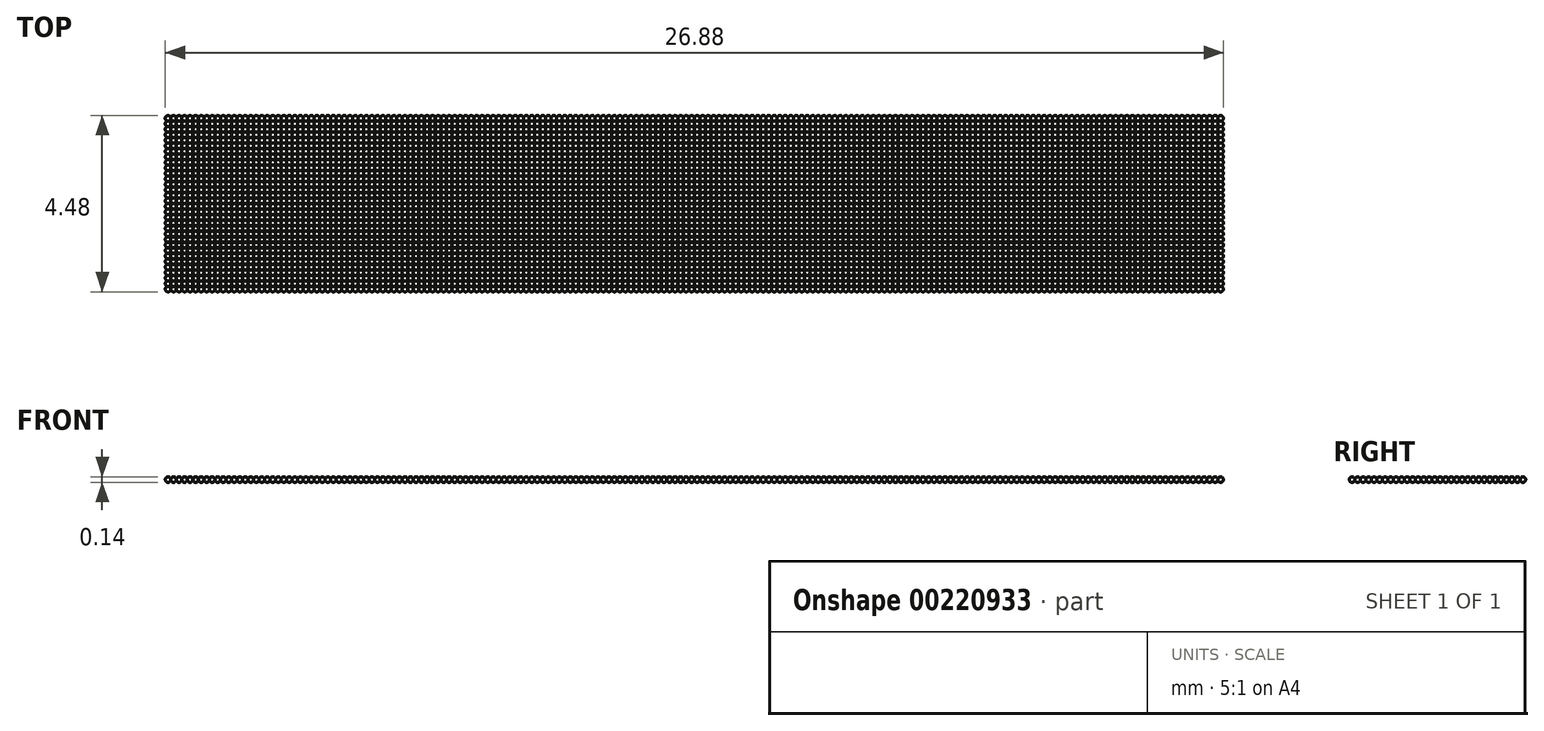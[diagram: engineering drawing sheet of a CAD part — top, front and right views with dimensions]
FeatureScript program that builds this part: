
annotation { "Feature Type Name" : "Feature", "Feature Type Description" : "" }
export const myFeature = defineFeature(function(context is Context, id is Id, definition is map)
    precondition{}
    {
        {
            var Q0;
            Q0=qCreatedBy(makeId("Front.planeOp"),FACE);
            var sketch = newSketch(context, id + "F0", { "sketchPlane" : qUnion([Q0])});
            skLineSegment(sketch, "E0", {"start": v(0, 0) * mm, "end": v(0.14, 0) * mm});
            skArc(sketch, "E1", {"start": v(0.14, 0) * mm, "mid": v(0.07, 0.07) * mm, "end": v(0, 0) * mm});
            skSolve(sketch);
        }
        {
            var Q0;
            Q0=sQuery(id+"F0.wireOp",EDGE,"E1");
            var Q1;
            Q1=sQuery(id+"F0.wireOp",EDGE,"E0");
            revolve(context, id + "F1", {"bodyType" : ToolBodyType.SURFACE, "surfaceEntities" : qUnion([Q0]), "axis" : qUnion([Q1]), "revolveType" : RevolveType.FULL});
        }
        {
            var Q0;
            Q0=makeQuery(id+"F1.opRevolve","SWEPT_BODY",BODY,{"disambiguationData":[OSD([sQuery(id+"F0.wireOp",EDGE,"E1")])]});
            transform(context, id + "F2", {"entities" : qUnion([Q0]), "transformType" : TransformType.TRANSLATION_3D, "dx" : 0.14 * mm, "dy" : 0 * mm, "dz" : 0 * mm, "makeCopy" : true});
        }
        {
            var Q0;
            Q0=makeQuery(id+"F2.opPattern","COPY",BODY,{"derivedFrom":makeQuery(id+"F1.opRevolve","SWEPT_BODY",BODY,{"disambiguationData":[OSD([sQuery(id+"F0.wireOp",EDGE,"E1")])]}),"instanceName":"1"});
            transform(context, id + "F3", {"entities" : qUnion([Q0]), "transformType" : TransformType.TRANSLATION_3D, "dx" : 0.14 * mm, "dy" : 0 * mm, "dz" : 0 * mm, "makeCopy" : true});
        }
        {
            var Q0;
            Q0=makeQuery(id+"F1.opRevolve","SWEPT_BODY",BODY,{"disambiguationData":[OSD([sQuery(id+"F0.wireOp",EDGE,"E1")])]});
            var Q1;
            Q1=makeQuery(id+"F2.opPattern","COPY",BODY,{"derivedFrom":makeQuery(id+"F1.opRevolve","SWEPT_BODY",BODY,{"disambiguationData":[OSD([sQuery(id+"F0.wireOp",EDGE,"E1")])]}),"instanceName":"1"});
            var Q2;
            Q2=makeQuery(id+"F3.opPattern","COPY",BODY,{"derivedFrom":makeQuery(id+"F2.opPattern","COPY",BODY,{"derivedFrom":makeQuery(id+"F1.opRevolve","SWEPT_BODY",BODY,{"disambiguationData":[OSD([sQuery(id+"F0.wireOp",EDGE,"E1")])]}),"instanceName":"1"}),"instanceName":"1"});
            transform(context, id + "F4", {"entities" : qUnion([Q0, Q1, Q2]), "transformType" : TransformType.TRANSLATION_3D, "dx" : 0.42 * mm, "dy" : 0 * mm, "dz" : 0 * mm, "makeCopy" : true});
        }
        {
            var Q0;
            Q0=makeQuery(id+"F1.opRevolve","SWEPT_BODY",BODY,{"disambiguationData":[OSD([sQuery(id+"F0.wireOp",EDGE,"E1")])]});
            var Q1;
            Q1=makeQuery(id+"F2.opPattern","COPY",BODY,{"derivedFrom":makeQuery(id+"F1.opRevolve","SWEPT_BODY",BODY,{"disambiguationData":[OSD([sQuery(id+"F0.wireOp",EDGE,"E1")])]}),"instanceName":"1"});
            var Q2;
            Q2=makeQuery(id+"F3.opPattern","COPY",BODY,{"derivedFrom":makeQuery(id+"F2.opPattern","COPY",BODY,{"derivedFrom":makeQuery(id+"F1.opRevolve","SWEPT_BODY",BODY,{"disambiguationData":[OSD([sQuery(id+"F0.wireOp",EDGE,"E1")])]}),"instanceName":"1"}),"instanceName":"1"});
            var Q3;
            Q3=makeQuery(id+"F4.opPattern","COPY",BODY,{"derivedFrom":makeQuery(id+"F1.opRevolve","SWEPT_BODY",BODY,{"disambiguationData":[OSD([sQuery(id+"F0.wireOp",EDGE,"E1")])]}),"instanceName":"1"});
            var Q4;
            Q4=makeQuery(id+"F4.opPattern","COPY",BODY,{"derivedFrom":makeQuery(id+"F2.opPattern","COPY",BODY,{"derivedFrom":makeQuery(id+"F1.opRevolve","SWEPT_BODY",BODY,{"disambiguationData":[OSD([sQuery(id+"F0.wireOp",EDGE,"E1")])]}),"instanceName":"1"}),"instanceName":"1"});
            var Q5;
            Q5=makeQuery(id+"F4.opPattern","COPY",BODY,{"derivedFrom":makeQuery(id+"F3.opPattern","COPY",BODY,{"derivedFrom":makeQuery(id+"F2.opPattern","COPY",BODY,{"derivedFrom":makeQuery(id+"F1.opRevolve","SWEPT_BODY",BODY,{"disambiguationData":[OSD([sQuery(id+"F0.wireOp",EDGE,"E1")])]}),"instanceName":"1"}),"instanceName":"1"}),"instanceName":"1"});
            transform(context, id + "F5", {"entities" : qUnion([Q0, Q1, Q2, Q3, Q4, Q5]), "transformType" : TransformType.TRANSLATION_3D, "dx" : 0.84 * mm, "dy" : 0 * mm, "dz" : 0 * mm, "makeCopy" : true});
        }
        {
            var Q0;
            Q0=makeQuery(id+"F1.opRevolve","SWEPT_BODY",BODY,{"disambiguationData":[OSD([sQuery(id+"F0.wireOp",EDGE,"E1")])]});
            var Q1;
            Q1=makeQuery(id+"F2.opPattern","COPY",BODY,{"derivedFrom":makeQuery(id+"F1.opRevolve","SWEPT_BODY",BODY,{"disambiguationData":[OSD([sQuery(id+"F0.wireOp",EDGE,"E1")])]}),"instanceName":"1"});
            var Q2;
            Q2=makeQuery(id+"F3.opPattern","COPY",BODY,{"derivedFrom":makeQuery(id+"F2.opPattern","COPY",BODY,{"derivedFrom":makeQuery(id+"F1.opRevolve","SWEPT_BODY",BODY,{"disambiguationData":[OSD([sQuery(id+"F0.wireOp",EDGE,"E1")])]}),"instanceName":"1"}),"instanceName":"1"});
            var Q3;
            Q3=makeQuery(id+"F4.opPattern","COPY",BODY,{"derivedFrom":makeQuery(id+"F1.opRevolve","SWEPT_BODY",BODY,{"disambiguationData":[OSD([sQuery(id+"F0.wireOp",EDGE,"E1")])]}),"instanceName":"1"});
            var Q4;
            Q4=makeQuery(id+"F4.opPattern","COPY",BODY,{"derivedFrom":makeQuery(id+"F2.opPattern","COPY",BODY,{"derivedFrom":makeQuery(id+"F1.opRevolve","SWEPT_BODY",BODY,{"disambiguationData":[OSD([sQuery(id+"F0.wireOp",EDGE,"E1")])]}),"instanceName":"1"}),"instanceName":"1"});
            var Q5;
            Q5=makeQuery(id+"F4.opPattern","COPY",BODY,{"derivedFrom":makeQuery(id+"F3.opPattern","COPY",BODY,{"derivedFrom":makeQuery(id+"F2.opPattern","COPY",BODY,{"derivedFrom":makeQuery(id+"F1.opRevolve","SWEPT_BODY",BODY,{"disambiguationData":[OSD([sQuery(id+"F0.wireOp",EDGE,"E1")])]}),"instanceName":"1"}),"instanceName":"1"}),"instanceName":"1"});
            var Q6;
            Q6=makeQuery(id+"F5.opPattern","COPY",BODY,{"derivedFrom":makeQuery(id+"F1.opRevolve","SWEPT_BODY",BODY,{"disambiguationData":[OSD([sQuery(id+"F0.wireOp",EDGE,"E1")])]}),"instanceName":"1"});
            var Q7;
            Q7=makeQuery(id+"F5.opPattern","COPY",BODY,{"derivedFrom":makeQuery(id+"F2.opPattern","COPY",BODY,{"derivedFrom":makeQuery(id+"F1.opRevolve","SWEPT_BODY",BODY,{"disambiguationData":[OSD([sQuery(id+"F0.wireOp",EDGE,"E1")])]}),"instanceName":"1"}),"instanceName":"1"});
            var Q8;
            Q8=makeQuery(id+"F5.opPattern","COPY",BODY,{"derivedFrom":makeQuery(id+"F3.opPattern","COPY",BODY,{"derivedFrom":makeQuery(id+"F2.opPattern","COPY",BODY,{"derivedFrom":makeQuery(id+"F1.opRevolve","SWEPT_BODY",BODY,{"disambiguationData":[OSD([sQuery(id+"F0.wireOp",EDGE,"E1")])]}),"instanceName":"1"}),"instanceName":"1"}),"instanceName":"1"});
            var Q9;
            Q9=makeQuery(id+"F5.opPattern","COPY",BODY,{"derivedFrom":makeQuery(id+"F4.opPattern","COPY",BODY,{"derivedFrom":makeQuery(id+"F1.opRevolve","SWEPT_BODY",BODY,{"disambiguationData":[OSD([sQuery(id+"F0.wireOp",EDGE,"E1")])]}),"instanceName":"1"}),"instanceName":"1"});
            var Q10;
            Q10=makeQuery(id+"F5.opPattern","COPY",BODY,{"derivedFrom":makeQuery(id+"F4.opPattern","COPY",BODY,{"derivedFrom":makeQuery(id+"F2.opPattern","COPY",BODY,{"derivedFrom":makeQuery(id+"F1.opRevolve","SWEPT_BODY",BODY,{"disambiguationData":[OSD([sQuery(id+"F0.wireOp",EDGE,"E1")])]}),"instanceName":"1"}),"instanceName":"1"}),"instanceName":"1"});
            var Q11;
            Q11=makeQuery(id+"F5.opPattern","COPY",BODY,{"derivedFrom":makeQuery(id+"F4.opPattern","COPY",BODY,{"derivedFrom":makeQuery(id+"F3.opPattern","COPY",BODY,{"derivedFrom":makeQuery(id+"F2.opPattern","COPY",BODY,{"derivedFrom":makeQuery(id+"F1.opRevolve","SWEPT_BODY",BODY,{"disambiguationData":[OSD([sQuery(id+"F0.wireOp",EDGE,"E1")])]}),"instanceName":"1"}),"instanceName":"1"}),"instanceName":"1"}),"instanceName":"1"});
            transform(context, id + "F6", {"entities" : qUnion([Q0, Q1, Q2, Q3, Q4, Q5, Q6, Q7, Q8, Q9, Q10, Q11]), "transformType" : TransformType.TRANSLATION_3D, "dx" : 1.68 * mm, "dy" : 0 * mm, "dz" : 0 * mm, "makeCopy" : true});
        }
        {
            var Q0;
            Q0=makeQuery(id+"F1.opRevolve","SWEPT_BODY",BODY,{"disambiguationData":[OSD([sQuery(id+"F0.wireOp",EDGE,"E1")])]});
            var Q1;
            Q1=makeQuery(id+"F3.opPattern","COPY",BODY,{"derivedFrom":makeQuery(id+"F2.opPattern","COPY",BODY,{"derivedFrom":makeQuery(id+"F1.opRevolve","SWEPT_BODY",BODY,{"disambiguationData":[OSD([sQuery(id+"F0.wireOp",EDGE,"E1")])]}),"instanceName":"1"}),"instanceName":"1"});
            var Q2;
            Q2=makeQuery(id+"F2.opPattern","COPY",BODY,{"derivedFrom":makeQuery(id+"F1.opRevolve","SWEPT_BODY",BODY,{"disambiguationData":[OSD([sQuery(id+"F0.wireOp",EDGE,"E1")])]}),"instanceName":"1"});
            var Q3;
            Q3=makeQuery(id+"F4.opPattern","COPY",BODY,{"derivedFrom":makeQuery(id+"F1.opRevolve","SWEPT_BODY",BODY,{"disambiguationData":[OSD([sQuery(id+"F0.wireOp",EDGE,"E1")])]}),"instanceName":"1"});
            var Q4;
            Q4=makeQuery(id+"F5.opPattern","COPY",BODY,{"derivedFrom":makeQuery(id+"F1.opRevolve","SWEPT_BODY",BODY,{"disambiguationData":[OSD([sQuery(id+"F0.wireOp",EDGE,"E1")])]}),"instanceName":"1"});
            var Q5;
            Q5=makeQuery(id+"F4.opPattern","COPY",BODY,{"derivedFrom":makeQuery(id+"F2.opPattern","COPY",BODY,{"derivedFrom":makeQuery(id+"F1.opRevolve","SWEPT_BODY",BODY,{"disambiguationData":[OSD([sQuery(id+"F0.wireOp",EDGE,"E1")])]}),"instanceName":"1"}),"instanceName":"1"});
            var Q6;
            Q6=makeQuery(id+"F4.opPattern","COPY",BODY,{"derivedFrom":makeQuery(id+"F3.opPattern","COPY",BODY,{"derivedFrom":makeQuery(id+"F2.opPattern","COPY",BODY,{"derivedFrom":makeQuery(id+"F1.opRevolve","SWEPT_BODY",BODY,{"disambiguationData":[OSD([sQuery(id+"F0.wireOp",EDGE,"E1")])]}),"instanceName":"1"}),"instanceName":"1"}),"instanceName":"1"});
            var Q7;
            Q7=makeQuery(id+"F6.opPattern","COPY",BODY,{"derivedFrom":makeQuery(id+"F1.opRevolve","SWEPT_BODY",BODY,{"disambiguationData":[OSD([sQuery(id+"F0.wireOp",EDGE,"E1")])]}),"instanceName":"1"});
            var Q8;
            Q8=makeQuery(id+"F5.opPattern","COPY",BODY,{"derivedFrom":makeQuery(id+"F2.opPattern","COPY",BODY,{"derivedFrom":makeQuery(id+"F1.opRevolve","SWEPT_BODY",BODY,{"disambiguationData":[OSD([sQuery(id+"F0.wireOp",EDGE,"E1")])]}),"instanceName":"1"}),"instanceName":"1"});
            var Q9;
            Q9=makeQuery(id+"F5.opPattern","COPY",BODY,{"derivedFrom":makeQuery(id+"F3.opPattern","COPY",BODY,{"derivedFrom":makeQuery(id+"F2.opPattern","COPY",BODY,{"derivedFrom":makeQuery(id+"F1.opRevolve","SWEPT_BODY",BODY,{"disambiguationData":[OSD([sQuery(id+"F0.wireOp",EDGE,"E1")])]}),"instanceName":"1"}),"instanceName":"1"}),"instanceName":"1"});
            var Q10;
            Q10=makeQuery(id+"F5.opPattern","COPY",BODY,{"derivedFrom":makeQuery(id+"F4.opPattern","COPY",BODY,{"derivedFrom":makeQuery(id+"F1.opRevolve","SWEPT_BODY",BODY,{"disambiguationData":[OSD([sQuery(id+"F0.wireOp",EDGE,"E1")])]}),"instanceName":"1"}),"instanceName":"1"});
            var Q11;
            Q11=makeQuery(id+"F5.opPattern","COPY",BODY,{"derivedFrom":makeQuery(id+"F4.opPattern","COPY",BODY,{"derivedFrom":makeQuery(id+"F2.opPattern","COPY",BODY,{"derivedFrom":makeQuery(id+"F1.opRevolve","SWEPT_BODY",BODY,{"disambiguationData":[OSD([sQuery(id+"F0.wireOp",EDGE,"E1")])]}),"instanceName":"1"}),"instanceName":"1"}),"instanceName":"1"});
            var Q12;
            Q12=makeQuery(id+"F5.opPattern","COPY",BODY,{"derivedFrom":makeQuery(id+"F4.opPattern","COPY",BODY,{"derivedFrom":makeQuery(id+"F3.opPattern","COPY",BODY,{"derivedFrom":makeQuery(id+"F2.opPattern","COPY",BODY,{"derivedFrom":makeQuery(id+"F1.opRevolve","SWEPT_BODY",BODY,{"disambiguationData":[OSD([sQuery(id+"F0.wireOp",EDGE,"E1")])]}),"instanceName":"1"}),"instanceName":"1"}),"instanceName":"1"}),"instanceName":"1"});
            var Q13;
            Q13=makeQuery(id+"F6.opPattern","COPY",BODY,{"derivedFrom":makeQuery(id+"F2.opPattern","COPY",BODY,{"derivedFrom":makeQuery(id+"F1.opRevolve","SWEPT_BODY",BODY,{"disambiguationData":[OSD([sQuery(id+"F0.wireOp",EDGE,"E1")])]}),"instanceName":"1"}),"instanceName":"1"});
            var Q14;
            Q14=makeQuery(id+"F6.opPattern","COPY",BODY,{"derivedFrom":makeQuery(id+"F3.opPattern","COPY",BODY,{"derivedFrom":makeQuery(id+"F2.opPattern","COPY",BODY,{"derivedFrom":makeQuery(id+"F1.opRevolve","SWEPT_BODY",BODY,{"disambiguationData":[OSD([sQuery(id+"F0.wireOp",EDGE,"E1")])]}),"instanceName":"1"}),"instanceName":"1"}),"instanceName":"1"});
            var Q15;
            Q15=makeQuery(id+"F6.opPattern","COPY",BODY,{"derivedFrom":makeQuery(id+"F4.opPattern","COPY",BODY,{"derivedFrom":makeQuery(id+"F1.opRevolve","SWEPT_BODY",BODY,{"disambiguationData":[OSD([sQuery(id+"F0.wireOp",EDGE,"E1")])]}),"instanceName":"1"}),"instanceName":"1"});
            var Q16;
            Q16=makeQuery(id+"F6.opPattern","COPY",BODY,{"derivedFrom":makeQuery(id+"F4.opPattern","COPY",BODY,{"derivedFrom":makeQuery(id+"F2.opPattern","COPY",BODY,{"derivedFrom":makeQuery(id+"F1.opRevolve","SWEPT_BODY",BODY,{"disambiguationData":[OSD([sQuery(id+"F0.wireOp",EDGE,"E1")])]}),"instanceName":"1"}),"instanceName":"1"}),"instanceName":"1"});
            var Q17;
            Q17=makeQuery(id+"F6.opPattern","COPY",BODY,{"derivedFrom":makeQuery(id+"F4.opPattern","COPY",BODY,{"derivedFrom":makeQuery(id+"F3.opPattern","COPY",BODY,{"derivedFrom":makeQuery(id+"F2.opPattern","COPY",BODY,{"derivedFrom":makeQuery(id+"F1.opRevolve","SWEPT_BODY",BODY,{"disambiguationData":[OSD([sQuery(id+"F0.wireOp",EDGE,"E1")])]}),"instanceName":"1"}),"instanceName":"1"}),"instanceName":"1"}),"instanceName":"1"});
            var Q18;
            Q18=makeQuery(id+"F6.opPattern","COPY",BODY,{"derivedFrom":makeQuery(id+"F5.opPattern","COPY",BODY,{"derivedFrom":makeQuery(id+"F1.opRevolve","SWEPT_BODY",BODY,{"disambiguationData":[OSD([sQuery(id+"F0.wireOp",EDGE,"E1")])]}),"instanceName":"1"}),"instanceName":"1"});
            var Q19;
            Q19=makeQuery(id+"F6.opPattern","COPY",BODY,{"derivedFrom":makeQuery(id+"F5.opPattern","COPY",BODY,{"derivedFrom":makeQuery(id+"F2.opPattern","COPY",BODY,{"derivedFrom":makeQuery(id+"F1.opRevolve","SWEPT_BODY",BODY,{"disambiguationData":[OSD([sQuery(id+"F0.wireOp",EDGE,"E1")])]}),"instanceName":"1"}),"instanceName":"1"}),"instanceName":"1"});
            var Q20;
            Q20=makeQuery(id+"F6.opPattern","COPY",BODY,{"derivedFrom":makeQuery(id+"F5.opPattern","COPY",BODY,{"derivedFrom":makeQuery(id+"F3.opPattern","COPY",BODY,{"derivedFrom":makeQuery(id+"F2.opPattern","COPY",BODY,{"derivedFrom":makeQuery(id+"F1.opRevolve","SWEPT_BODY",BODY,{"disambiguationData":[OSD([sQuery(id+"F0.wireOp",EDGE,"E1")])]}),"instanceName":"1"}),"instanceName":"1"}),"instanceName":"1"}),"instanceName":"1"});
            var Q21;
            Q21=makeQuery(id+"F6.opPattern","COPY",BODY,{"derivedFrom":makeQuery(id+"F5.opPattern","COPY",BODY,{"derivedFrom":makeQuery(id+"F4.opPattern","COPY",BODY,{"derivedFrom":makeQuery(id+"F1.opRevolve","SWEPT_BODY",BODY,{"disambiguationData":[OSD([sQuery(id+"F0.wireOp",EDGE,"E1")])]}),"instanceName":"1"}),"instanceName":"1"}),"instanceName":"1"});
            var Q22;
            Q22=makeQuery(id+"F6.opPattern","COPY",BODY,{"derivedFrom":makeQuery(id+"F5.opPattern","COPY",BODY,{"derivedFrom":makeQuery(id+"F4.opPattern","COPY",BODY,{"derivedFrom":makeQuery(id+"F2.opPattern","COPY",BODY,{"derivedFrom":makeQuery(id+"F1.opRevolve","SWEPT_BODY",BODY,{"disambiguationData":[OSD([sQuery(id+"F0.wireOp",EDGE,"E1")])]}),"instanceName":"1"}),"instanceName":"1"}),"instanceName":"1"}),"instanceName":"1"});
            var Q23;
            Q23=makeQuery(id+"F6.opPattern","COPY",BODY,{"derivedFrom":makeQuery(id+"F5.opPattern","COPY",BODY,{"derivedFrom":makeQuery(id+"F4.opPattern","COPY",BODY,{"derivedFrom":makeQuery(id+"F3.opPattern","COPY",BODY,{"derivedFrom":makeQuery(id+"F2.opPattern","COPY",BODY,{"derivedFrom":makeQuery(id+"F1.opRevolve","SWEPT_BODY",BODY,{"disambiguationData":[OSD([sQuery(id+"F0.wireOp",EDGE,"E1")])]}),"instanceName":"1"}),"instanceName":"1"}),"instanceName":"1"}),"instanceName":"1"}),"instanceName":"1"});
            transform(context, id + "F7", {"entities" : qUnion([Q0, Q1, Q2, Q3, Q4, Q5, Q6, Q7, Q8, Q9, Q10, Q11, Q12, Q13, Q14, Q15, Q16, Q17, Q18, Q19, Q20, Q21, Q22, Q23]), "transformType" : TransformType.TRANSLATION_3D, "dx" : 3.36 * mm, "dy" : 0 * mm, "dz" : 0 * mm, "makeCopy" : true});
        }
        {
            var Q0;
            Q0=makeQuery(id+"F1.opRevolve","SWEPT_BODY",BODY,{"disambiguationData":[OSD([sQuery(id+"F0.wireOp",EDGE,"E1")])]});
            var Q1;
            Q1=makeQuery(id+"F3.opPattern","COPY",BODY,{"derivedFrom":makeQuery(id+"F2.opPattern","COPY",BODY,{"derivedFrom":makeQuery(id+"F1.opRevolve","SWEPT_BODY",BODY,{"disambiguationData":[OSD([sQuery(id+"F0.wireOp",EDGE,"E1")])]}),"instanceName":"1"}),"instanceName":"1"});
            var Q2;
            Q2=makeQuery(id+"F2.opPattern","COPY",BODY,{"derivedFrom":makeQuery(id+"F1.opRevolve","SWEPT_BODY",BODY,{"disambiguationData":[OSD([sQuery(id+"F0.wireOp",EDGE,"E1")])]}),"instanceName":"1"});
            var Q3;
            Q3=makeQuery(id+"F4.opPattern","COPY",BODY,{"derivedFrom":makeQuery(id+"F1.opRevolve","SWEPT_BODY",BODY,{"disambiguationData":[OSD([sQuery(id+"F0.wireOp",EDGE,"E1")])]}),"instanceName":"1"});
            var Q4;
            Q4=makeQuery(id+"F5.opPattern","COPY",BODY,{"derivedFrom":makeQuery(id+"F1.opRevolve","SWEPT_BODY",BODY,{"disambiguationData":[OSD([sQuery(id+"F0.wireOp",EDGE,"E1")])]}),"instanceName":"1"});
            var Q5;
            Q5=makeQuery(id+"F4.opPattern","COPY",BODY,{"derivedFrom":makeQuery(id+"F2.opPattern","COPY",BODY,{"derivedFrom":makeQuery(id+"F1.opRevolve","SWEPT_BODY",BODY,{"disambiguationData":[OSD([sQuery(id+"F0.wireOp",EDGE,"E1")])]}),"instanceName":"1"}),"instanceName":"1"});
            var Q6;
            Q6=makeQuery(id+"F4.opPattern","COPY",BODY,{"derivedFrom":makeQuery(id+"F3.opPattern","COPY",BODY,{"derivedFrom":makeQuery(id+"F2.opPattern","COPY",BODY,{"derivedFrom":makeQuery(id+"F1.opRevolve","SWEPT_BODY",BODY,{"disambiguationData":[OSD([sQuery(id+"F0.wireOp",EDGE,"E1")])]}),"instanceName":"1"}),"instanceName":"1"}),"instanceName":"1"});
            var Q7;
            Q7=makeQuery(id+"F7.opPattern","COPY",BODY,{"derivedFrom":makeQuery(id+"F4.opPattern","COPY",BODY,{"derivedFrom":makeQuery(id+"F3.opPattern","COPY",BODY,{"derivedFrom":makeQuery(id+"F2.opPattern","COPY",BODY,{"derivedFrom":makeQuery(id+"F1.opRevolve","SWEPT_BODY",BODY,{"disambiguationData":[OSD([sQuery(id+"F0.wireOp",EDGE,"E1")])]}),"instanceName":"1"}),"instanceName":"1"}),"instanceName":"1"}),"instanceName":"1"});
            var Q8;
            Q8=makeQuery(id+"F7.opPattern","COPY",BODY,{"derivedFrom":makeQuery(id+"F4.opPattern","COPY",BODY,{"derivedFrom":makeQuery(id+"F2.opPattern","COPY",BODY,{"derivedFrom":makeQuery(id+"F1.opRevolve","SWEPT_BODY",BODY,{"disambiguationData":[OSD([sQuery(id+"F0.wireOp",EDGE,"E1")])]}),"instanceName":"1"}),"instanceName":"1"}),"instanceName":"1"});
            var Q9;
            Q9=makeQuery(id+"F7.opPattern","COPY",BODY,{"derivedFrom":makeQuery(id+"F4.opPattern","COPY",BODY,{"derivedFrom":makeQuery(id+"F1.opRevolve","SWEPT_BODY",BODY,{"disambiguationData":[OSD([sQuery(id+"F0.wireOp",EDGE,"E1")])]}),"instanceName":"1"}),"instanceName":"1"});
            var Q10;
            Q10=makeQuery(id+"F7.opPattern","COPY",BODY,{"derivedFrom":makeQuery(id+"F3.opPattern","COPY",BODY,{"derivedFrom":makeQuery(id+"F2.opPattern","COPY",BODY,{"derivedFrom":makeQuery(id+"F1.opRevolve","SWEPT_BODY",BODY,{"disambiguationData":[OSD([sQuery(id+"F0.wireOp",EDGE,"E1")])]}),"instanceName":"1"}),"instanceName":"1"}),"instanceName":"1"});
            var Q11;
            Q11=makeQuery(id+"F7.opPattern","COPY",BODY,{"derivedFrom":makeQuery(id+"F2.opPattern","COPY",BODY,{"derivedFrom":makeQuery(id+"F1.opRevolve","SWEPT_BODY",BODY,{"disambiguationData":[OSD([sQuery(id+"F0.wireOp",EDGE,"E1")])]}),"instanceName":"1"}),"instanceName":"1"});
            var Q12;
            Q12=makeQuery(id+"F7.opPattern","COPY",BODY,{"derivedFrom":makeQuery(id+"F1.opRevolve","SWEPT_BODY",BODY,{"disambiguationData":[OSD([sQuery(id+"F0.wireOp",EDGE,"E1")])]}),"instanceName":"1"});
            var Q13;
            Q13=makeQuery(id+"F6.opPattern","COPY",BODY,{"derivedFrom":makeQuery(id+"F1.opRevolve","SWEPT_BODY",BODY,{"disambiguationData":[OSD([sQuery(id+"F0.wireOp",EDGE,"E1")])]}),"instanceName":"1"});
            var Q14;
            Q14=makeQuery(id+"F5.opPattern","COPY",BODY,{"derivedFrom":makeQuery(id+"F2.opPattern","COPY",BODY,{"derivedFrom":makeQuery(id+"F1.opRevolve","SWEPT_BODY",BODY,{"disambiguationData":[OSD([sQuery(id+"F0.wireOp",EDGE,"E1")])]}),"instanceName":"1"}),"instanceName":"1"});
            var Q15;
            Q15=makeQuery(id+"F5.opPattern","COPY",BODY,{"derivedFrom":makeQuery(id+"F3.opPattern","COPY",BODY,{"derivedFrom":makeQuery(id+"F2.opPattern","COPY",BODY,{"derivedFrom":makeQuery(id+"F1.opRevolve","SWEPT_BODY",BODY,{"disambiguationData":[OSD([sQuery(id+"F0.wireOp",EDGE,"E1")])]}),"instanceName":"1"}),"instanceName":"1"}),"instanceName":"1"});
            var Q16;
            Q16=makeQuery(id+"F5.opPattern","COPY",BODY,{"derivedFrom":makeQuery(id+"F4.opPattern","COPY",BODY,{"derivedFrom":makeQuery(id+"F1.opRevolve","SWEPT_BODY",BODY,{"disambiguationData":[OSD([sQuery(id+"F0.wireOp",EDGE,"E1")])]}),"instanceName":"1"}),"instanceName":"1"});
            var Q17;
            Q17=makeQuery(id+"F5.opPattern","COPY",BODY,{"derivedFrom":makeQuery(id+"F4.opPattern","COPY",BODY,{"derivedFrom":makeQuery(id+"F2.opPattern","COPY",BODY,{"derivedFrom":makeQuery(id+"F1.opRevolve","SWEPT_BODY",BODY,{"disambiguationData":[OSD([sQuery(id+"F0.wireOp",EDGE,"E1")])]}),"instanceName":"1"}),"instanceName":"1"}),"instanceName":"1"});
            var Q18;
            Q18=makeQuery(id+"F5.opPattern","COPY",BODY,{"derivedFrom":makeQuery(id+"F4.opPattern","COPY",BODY,{"derivedFrom":makeQuery(id+"F3.opPattern","COPY",BODY,{"derivedFrom":makeQuery(id+"F2.opPattern","COPY",BODY,{"derivedFrom":makeQuery(id+"F1.opRevolve","SWEPT_BODY",BODY,{"disambiguationData":[OSD([sQuery(id+"F0.wireOp",EDGE,"E1")])]}),"instanceName":"1"}),"instanceName":"1"}),"instanceName":"1"}),"instanceName":"1"});
            var Q19;
            Q19=makeQuery(id+"F7.opPattern","COPY",BODY,{"derivedFrom":makeQuery(id+"F5.opPattern","COPY",BODY,{"derivedFrom":makeQuery(id+"F1.opRevolve","SWEPT_BODY",BODY,{"disambiguationData":[OSD([sQuery(id+"F0.wireOp",EDGE,"E1")])]}),"instanceName":"1"}),"instanceName":"1"});
            var Q20;
            Q20=makeQuery(id+"F6.opPattern","COPY",BODY,{"derivedFrom":makeQuery(id+"F2.opPattern","COPY",BODY,{"derivedFrom":makeQuery(id+"F1.opRevolve","SWEPT_BODY",BODY,{"disambiguationData":[OSD([sQuery(id+"F0.wireOp",EDGE,"E1")])]}),"instanceName":"1"}),"instanceName":"1"});
            var Q21;
            Q21=makeQuery(id+"F6.opPattern","COPY",BODY,{"derivedFrom":makeQuery(id+"F3.opPattern","COPY",BODY,{"derivedFrom":makeQuery(id+"F2.opPattern","COPY",BODY,{"derivedFrom":makeQuery(id+"F1.opRevolve","SWEPT_BODY",BODY,{"disambiguationData":[OSD([sQuery(id+"F0.wireOp",EDGE,"E1")])]}),"instanceName":"1"}),"instanceName":"1"}),"instanceName":"1"});
            var Q22;
            Q22=makeQuery(id+"F6.opPattern","COPY",BODY,{"derivedFrom":makeQuery(id+"F4.opPattern","COPY",BODY,{"derivedFrom":makeQuery(id+"F1.opRevolve","SWEPT_BODY",BODY,{"disambiguationData":[OSD([sQuery(id+"F0.wireOp",EDGE,"E1")])]}),"instanceName":"1"}),"instanceName":"1"});
            var Q23;
            Q23=makeQuery(id+"F6.opPattern","COPY",BODY,{"derivedFrom":makeQuery(id+"F4.opPattern","COPY",BODY,{"derivedFrom":makeQuery(id+"F2.opPattern","COPY",BODY,{"derivedFrom":makeQuery(id+"F1.opRevolve","SWEPT_BODY",BODY,{"disambiguationData":[OSD([sQuery(id+"F0.wireOp",EDGE,"E1")])]}),"instanceName":"1"}),"instanceName":"1"}),"instanceName":"1"});
            var Q24;
            Q24=makeQuery(id+"F6.opPattern","COPY",BODY,{"derivedFrom":makeQuery(id+"F4.opPattern","COPY",BODY,{"derivedFrom":makeQuery(id+"F3.opPattern","COPY",BODY,{"derivedFrom":makeQuery(id+"F2.opPattern","COPY",BODY,{"derivedFrom":makeQuery(id+"F1.opRevolve","SWEPT_BODY",BODY,{"disambiguationData":[OSD([sQuery(id+"F0.wireOp",EDGE,"E1")])]}),"instanceName":"1"}),"instanceName":"1"}),"instanceName":"1"}),"instanceName":"1"});
            var Q25;
            Q25=makeQuery(id+"F6.opPattern","COPY",BODY,{"derivedFrom":makeQuery(id+"F5.opPattern","COPY",BODY,{"derivedFrom":makeQuery(id+"F1.opRevolve","SWEPT_BODY",BODY,{"disambiguationData":[OSD([sQuery(id+"F0.wireOp",EDGE,"E1")])]}),"instanceName":"1"}),"instanceName":"1"});
            var Q26;
            Q26=makeQuery(id+"F6.opPattern","COPY",BODY,{"derivedFrom":makeQuery(id+"F5.opPattern","COPY",BODY,{"derivedFrom":makeQuery(id+"F2.opPattern","COPY",BODY,{"derivedFrom":makeQuery(id+"F1.opRevolve","SWEPT_BODY",BODY,{"disambiguationData":[OSD([sQuery(id+"F0.wireOp",EDGE,"E1")])]}),"instanceName":"1"}),"instanceName":"1"}),"instanceName":"1"});
            var Q27;
            Q27=makeQuery(id+"F6.opPattern","COPY",BODY,{"derivedFrom":makeQuery(id+"F5.opPattern","COPY",BODY,{"derivedFrom":makeQuery(id+"F3.opPattern","COPY",BODY,{"derivedFrom":makeQuery(id+"F2.opPattern","COPY",BODY,{"derivedFrom":makeQuery(id+"F1.opRevolve","SWEPT_BODY",BODY,{"disambiguationData":[OSD([sQuery(id+"F0.wireOp",EDGE,"E1")])]}),"instanceName":"1"}),"instanceName":"1"}),"instanceName":"1"}),"instanceName":"1"});
            var Q28;
            Q28=makeQuery(id+"F6.opPattern","COPY",BODY,{"derivedFrom":makeQuery(id+"F5.opPattern","COPY",BODY,{"derivedFrom":makeQuery(id+"F4.opPattern","COPY",BODY,{"derivedFrom":makeQuery(id+"F1.opRevolve","SWEPT_BODY",BODY,{"disambiguationData":[OSD([sQuery(id+"F0.wireOp",EDGE,"E1")])]}),"instanceName":"1"}),"instanceName":"1"}),"instanceName":"1"});
            var Q29;
            Q29=makeQuery(id+"F6.opPattern","COPY",BODY,{"derivedFrom":makeQuery(id+"F5.opPattern","COPY",BODY,{"derivedFrom":makeQuery(id+"F4.opPattern","COPY",BODY,{"derivedFrom":makeQuery(id+"F2.opPattern","COPY",BODY,{"derivedFrom":makeQuery(id+"F1.opRevolve","SWEPT_BODY",BODY,{"disambiguationData":[OSD([sQuery(id+"F0.wireOp",EDGE,"E1")])]}),"instanceName":"1"}),"instanceName":"1"}),"instanceName":"1"}),"instanceName":"1"});
            var Q30;
            Q30=makeQuery(id+"F6.opPattern","COPY",BODY,{"derivedFrom":makeQuery(id+"F5.opPattern","COPY",BODY,{"derivedFrom":makeQuery(id+"F4.opPattern","COPY",BODY,{"derivedFrom":makeQuery(id+"F3.opPattern","COPY",BODY,{"derivedFrom":makeQuery(id+"F2.opPattern","COPY",BODY,{"derivedFrom":makeQuery(id+"F1.opRevolve","SWEPT_BODY",BODY,{"disambiguationData":[OSD([sQuery(id+"F0.wireOp",EDGE,"E1")])]}),"instanceName":"1"}),"instanceName":"1"}),"instanceName":"1"}),"instanceName":"1"}),"instanceName":"1"});
            var Q31;
            Q31=makeQuery(id+"F7.opPattern","COPY",BODY,{"derivedFrom":makeQuery(id+"F5.opPattern","COPY",BODY,{"derivedFrom":makeQuery(id+"F2.opPattern","COPY",BODY,{"derivedFrom":makeQuery(id+"F1.opRevolve","SWEPT_BODY",BODY,{"disambiguationData":[OSD([sQuery(id+"F0.wireOp",EDGE,"E1")])]}),"instanceName":"1"}),"instanceName":"1"}),"instanceName":"1"});
            var Q32;
            Q32=makeQuery(id+"F7.opPattern","COPY",BODY,{"derivedFrom":makeQuery(id+"F5.opPattern","COPY",BODY,{"derivedFrom":makeQuery(id+"F3.opPattern","COPY",BODY,{"derivedFrom":makeQuery(id+"F2.opPattern","COPY",BODY,{"derivedFrom":makeQuery(id+"F1.opRevolve","SWEPT_BODY",BODY,{"disambiguationData":[OSD([sQuery(id+"F0.wireOp",EDGE,"E1")])]}),"instanceName":"1"}),"instanceName":"1"}),"instanceName":"1"}),"instanceName":"1"});
            var Q33;
            Q33=makeQuery(id+"F7.opPattern","COPY",BODY,{"derivedFrom":makeQuery(id+"F5.opPattern","COPY",BODY,{"derivedFrom":makeQuery(id+"F4.opPattern","COPY",BODY,{"derivedFrom":makeQuery(id+"F1.opRevolve","SWEPT_BODY",BODY,{"disambiguationData":[OSD([sQuery(id+"F0.wireOp",EDGE,"E1")])]}),"instanceName":"1"}),"instanceName":"1"}),"instanceName":"1"});
            var Q34;
            Q34=makeQuery(id+"F7.opPattern","COPY",BODY,{"derivedFrom":makeQuery(id+"F5.opPattern","COPY",BODY,{"derivedFrom":makeQuery(id+"F4.opPattern","COPY",BODY,{"derivedFrom":makeQuery(id+"F2.opPattern","COPY",BODY,{"derivedFrom":makeQuery(id+"F1.opRevolve","SWEPT_BODY",BODY,{"disambiguationData":[OSD([sQuery(id+"F0.wireOp",EDGE,"E1")])]}),"instanceName":"1"}),"instanceName":"1"}),"instanceName":"1"}),"instanceName":"1"});
            var Q35;
            Q35=makeQuery(id+"F7.opPattern","COPY",BODY,{"derivedFrom":makeQuery(id+"F5.opPattern","COPY",BODY,{"derivedFrom":makeQuery(id+"F4.opPattern","COPY",BODY,{"derivedFrom":makeQuery(id+"F3.opPattern","COPY",BODY,{"derivedFrom":makeQuery(id+"F2.opPattern","COPY",BODY,{"derivedFrom":makeQuery(id+"F1.opRevolve","SWEPT_BODY",BODY,{"disambiguationData":[OSD([sQuery(id+"F0.wireOp",EDGE,"E1")])]}),"instanceName":"1"}),"instanceName":"1"}),"instanceName":"1"}),"instanceName":"1"}),"instanceName":"1"});
            var Q36;
            Q36=makeQuery(id+"F7.opPattern","COPY",BODY,{"derivedFrom":makeQuery(id+"F6.opPattern","COPY",BODY,{"derivedFrom":makeQuery(id+"F1.opRevolve","SWEPT_BODY",BODY,{"disambiguationData":[OSD([sQuery(id+"F0.wireOp",EDGE,"E1")])]}),"instanceName":"1"}),"instanceName":"1"});
            var Q37;
            Q37=makeQuery(id+"F7.opPattern","COPY",BODY,{"derivedFrom":makeQuery(id+"F6.opPattern","COPY",BODY,{"derivedFrom":makeQuery(id+"F2.opPattern","COPY",BODY,{"derivedFrom":makeQuery(id+"F1.opRevolve","SWEPT_BODY",BODY,{"disambiguationData":[OSD([sQuery(id+"F0.wireOp",EDGE,"E1")])]}),"instanceName":"1"}),"instanceName":"1"}),"instanceName":"1"});
            var Q38;
            Q38=makeQuery(id+"F7.opPattern","COPY",BODY,{"derivedFrom":makeQuery(id+"F6.opPattern","COPY",BODY,{"derivedFrom":makeQuery(id+"F3.opPattern","COPY",BODY,{"derivedFrom":makeQuery(id+"F2.opPattern","COPY",BODY,{"derivedFrom":makeQuery(id+"F1.opRevolve","SWEPT_BODY",BODY,{"disambiguationData":[OSD([sQuery(id+"F0.wireOp",EDGE,"E1")])]}),"instanceName":"1"}),"instanceName":"1"}),"instanceName":"1"}),"instanceName":"1"});
            var Q39;
            Q39=makeQuery(id+"F7.opPattern","COPY",BODY,{"derivedFrom":makeQuery(id+"F6.opPattern","COPY",BODY,{"derivedFrom":makeQuery(id+"F4.opPattern","COPY",BODY,{"derivedFrom":makeQuery(id+"F1.opRevolve","SWEPT_BODY",BODY,{"disambiguationData":[OSD([sQuery(id+"F0.wireOp",EDGE,"E1")])]}),"instanceName":"1"}),"instanceName":"1"}),"instanceName":"1"});
            var Q40;
            Q40=makeQuery(id+"F7.opPattern","COPY",BODY,{"derivedFrom":makeQuery(id+"F6.opPattern","COPY",BODY,{"derivedFrom":makeQuery(id+"F4.opPattern","COPY",BODY,{"derivedFrom":makeQuery(id+"F2.opPattern","COPY",BODY,{"derivedFrom":makeQuery(id+"F1.opRevolve","SWEPT_BODY",BODY,{"disambiguationData":[OSD([sQuery(id+"F0.wireOp",EDGE,"E1")])]}),"instanceName":"1"}),"instanceName":"1"}),"instanceName":"1"}),"instanceName":"1"});
            var Q41;
            Q41=makeQuery(id+"F7.opPattern","COPY",BODY,{"derivedFrom":makeQuery(id+"F6.opPattern","COPY",BODY,{"derivedFrom":makeQuery(id+"F4.opPattern","COPY",BODY,{"derivedFrom":makeQuery(id+"F3.opPattern","COPY",BODY,{"derivedFrom":makeQuery(id+"F2.opPattern","COPY",BODY,{"derivedFrom":makeQuery(id+"F1.opRevolve","SWEPT_BODY",BODY,{"disambiguationData":[OSD([sQuery(id+"F0.wireOp",EDGE,"E1")])]}),"instanceName":"1"}),"instanceName":"1"}),"instanceName":"1"}),"instanceName":"1"}),"instanceName":"1"});
            var Q42;
            Q42=makeQuery(id+"F7.opPattern","COPY",BODY,{"derivedFrom":makeQuery(id+"F6.opPattern","COPY",BODY,{"derivedFrom":makeQuery(id+"F5.opPattern","COPY",BODY,{"derivedFrom":makeQuery(id+"F1.opRevolve","SWEPT_BODY",BODY,{"disambiguationData":[OSD([sQuery(id+"F0.wireOp",EDGE,"E1")])]}),"instanceName":"1"}),"instanceName":"1"}),"instanceName":"1"});
            var Q43;
            Q43=makeQuery(id+"F7.opPattern","COPY",BODY,{"derivedFrom":makeQuery(id+"F6.opPattern","COPY",BODY,{"derivedFrom":makeQuery(id+"F5.opPattern","COPY",BODY,{"derivedFrom":makeQuery(id+"F2.opPattern","COPY",BODY,{"derivedFrom":makeQuery(id+"F1.opRevolve","SWEPT_BODY",BODY,{"disambiguationData":[OSD([sQuery(id+"F0.wireOp",EDGE,"E1")])]}),"instanceName":"1"}),"instanceName":"1"}),"instanceName":"1"}),"instanceName":"1"});
            var Q44;
            Q44=makeQuery(id+"F7.opPattern","COPY",BODY,{"derivedFrom":makeQuery(id+"F6.opPattern","COPY",BODY,{"derivedFrom":makeQuery(id+"F5.opPattern","COPY",BODY,{"derivedFrom":makeQuery(id+"F3.opPattern","COPY",BODY,{"derivedFrom":makeQuery(id+"F2.opPattern","COPY",BODY,{"derivedFrom":makeQuery(id+"F1.opRevolve","SWEPT_BODY",BODY,{"disambiguationData":[OSD([sQuery(id+"F0.wireOp",EDGE,"E1")])]}),"instanceName":"1"}),"instanceName":"1"}),"instanceName":"1"}),"instanceName":"1"}),"instanceName":"1"});
            var Q45;
            Q45=makeQuery(id+"F7.opPattern","COPY",BODY,{"derivedFrom":makeQuery(id+"F6.opPattern","COPY",BODY,{"derivedFrom":makeQuery(id+"F5.opPattern","COPY",BODY,{"derivedFrom":makeQuery(id+"F4.opPattern","COPY",BODY,{"derivedFrom":makeQuery(id+"F1.opRevolve","SWEPT_BODY",BODY,{"disambiguationData":[OSD([sQuery(id+"F0.wireOp",EDGE,"E1")])]}),"instanceName":"1"}),"instanceName":"1"}),"instanceName":"1"}),"instanceName":"1"});
            var Q46;
            Q46=makeQuery(id+"F7.opPattern","COPY",BODY,{"derivedFrom":makeQuery(id+"F6.opPattern","COPY",BODY,{"derivedFrom":makeQuery(id+"F5.opPattern","COPY",BODY,{"derivedFrom":makeQuery(id+"F4.opPattern","COPY",BODY,{"derivedFrom":makeQuery(id+"F2.opPattern","COPY",BODY,{"derivedFrom":makeQuery(id+"F1.opRevolve","SWEPT_BODY",BODY,{"disambiguationData":[OSD([sQuery(id+"F0.wireOp",EDGE,"E1")])]}),"instanceName":"1"}),"instanceName":"1"}),"instanceName":"1"}),"instanceName":"1"}),"instanceName":"1"});
            var Q47;
            Q47=makeQuery(id+"F7.opPattern","COPY",BODY,{"derivedFrom":makeQuery(id+"F6.opPattern","COPY",BODY,{"derivedFrom":makeQuery(id+"F5.opPattern","COPY",BODY,{"derivedFrom":makeQuery(id+"F4.opPattern","COPY",BODY,{"derivedFrom":makeQuery(id+"F3.opPattern","COPY",BODY,{"derivedFrom":makeQuery(id+"F2.opPattern","COPY",BODY,{"derivedFrom":makeQuery(id+"F1.opRevolve","SWEPT_BODY",BODY,{"disambiguationData":[OSD([sQuery(id+"F0.wireOp",EDGE,"E1")])]}),"instanceName":"1"}),"instanceName":"1"}),"instanceName":"1"}),"instanceName":"1"}),"instanceName":"1"}),"instanceName":"1"});
            transform(context, id + "F8", {"entities" : qUnion([Q0, Q1, Q2, Q3, Q4, Q5, Q6, Q7, Q8, Q9, Q10, Q11, Q12, Q13, Q14, Q15, Q16, Q17, Q18, Q19, Q20, Q21, Q22, Q23, Q24, Q25, Q26, Q27, Q28, Q29, Q30, Q31, Q32, Q33, Q34, Q35, Q36, Q37, Q38, Q39, Q40, Q41, Q42, Q43, Q44, Q45, Q46, Q47]), "transformType" : TransformType.TRANSLATION_3D, "dx" : 6.72 * mm, "dy" : 0 * mm, "dz" : 0 * mm, "makeCopy" : true});
        }
        {
            var Q0;
            Q0=makeQuery(id+"F1.opRevolve","SWEPT_BODY",BODY,{"disambiguationData":[OSD([sQuery(id+"F0.wireOp",EDGE,"E1")])]});
            var Q1;
            Q1=makeQuery(id+"F3.opPattern","COPY",BODY,{"derivedFrom":makeQuery(id+"F2.opPattern","COPY",BODY,{"derivedFrom":makeQuery(id+"F1.opRevolve","SWEPT_BODY",BODY,{"disambiguationData":[OSD([sQuery(id+"F0.wireOp",EDGE,"E1")])]}),"instanceName":"1"}),"instanceName":"1"});
            var Q2;
            Q2=makeQuery(id+"F2.opPattern","COPY",BODY,{"derivedFrom":makeQuery(id+"F1.opRevolve","SWEPT_BODY",BODY,{"disambiguationData":[OSD([sQuery(id+"F0.wireOp",EDGE,"E1")])]}),"instanceName":"1"});
            var Q3;
            Q3=makeQuery(id+"F4.opPattern","COPY",BODY,{"derivedFrom":makeQuery(id+"F1.opRevolve","SWEPT_BODY",BODY,{"disambiguationData":[OSD([sQuery(id+"F0.wireOp",EDGE,"E1")])]}),"instanceName":"1"});
            var Q4;
            Q4=makeQuery(id+"F5.opPattern","COPY",BODY,{"derivedFrom":makeQuery(id+"F1.opRevolve","SWEPT_BODY",BODY,{"disambiguationData":[OSD([sQuery(id+"F0.wireOp",EDGE,"E1")])]}),"instanceName":"1"});
            var Q5;
            Q5=makeQuery(id+"F4.opPattern","COPY",BODY,{"derivedFrom":makeQuery(id+"F2.opPattern","COPY",BODY,{"derivedFrom":makeQuery(id+"F1.opRevolve","SWEPT_BODY",BODY,{"disambiguationData":[OSD([sQuery(id+"F0.wireOp",EDGE,"E1")])]}),"instanceName":"1"}),"instanceName":"1"});
            var Q6;
            Q6=makeQuery(id+"F4.opPattern","COPY",BODY,{"derivedFrom":makeQuery(id+"F3.opPattern","COPY",BODY,{"derivedFrom":makeQuery(id+"F2.opPattern","COPY",BODY,{"derivedFrom":makeQuery(id+"F1.opRevolve","SWEPT_BODY",BODY,{"disambiguationData":[OSD([sQuery(id+"F0.wireOp",EDGE,"E1")])]}),"instanceName":"1"}),"instanceName":"1"}),"instanceName":"1"});
            var Q7;
            Q7=makeQuery(id+"F7.opPattern","COPY",BODY,{"derivedFrom":makeQuery(id+"F4.opPattern","COPY",BODY,{"derivedFrom":makeQuery(id+"F3.opPattern","COPY",BODY,{"derivedFrom":makeQuery(id+"F2.opPattern","COPY",BODY,{"derivedFrom":makeQuery(id+"F1.opRevolve","SWEPT_BODY",BODY,{"disambiguationData":[OSD([sQuery(id+"F0.wireOp",EDGE,"E1")])]}),"instanceName":"1"}),"instanceName":"1"}),"instanceName":"1"}),"instanceName":"1"});
            var Q8;
            Q8=makeQuery(id+"F7.opPattern","COPY",BODY,{"derivedFrom":makeQuery(id+"F4.opPattern","COPY",BODY,{"derivedFrom":makeQuery(id+"F2.opPattern","COPY",BODY,{"derivedFrom":makeQuery(id+"F1.opRevolve","SWEPT_BODY",BODY,{"disambiguationData":[OSD([sQuery(id+"F0.wireOp",EDGE,"E1")])]}),"instanceName":"1"}),"instanceName":"1"}),"instanceName":"1"});
            var Q9;
            Q9=makeQuery(id+"F7.opPattern","COPY",BODY,{"derivedFrom":makeQuery(id+"F4.opPattern","COPY",BODY,{"derivedFrom":makeQuery(id+"F1.opRevolve","SWEPT_BODY",BODY,{"disambiguationData":[OSD([sQuery(id+"F0.wireOp",EDGE,"E1")])]}),"instanceName":"1"}),"instanceName":"1"});
            var Q10;
            Q10=makeQuery(id+"F7.opPattern","COPY",BODY,{"derivedFrom":makeQuery(id+"F3.opPattern","COPY",BODY,{"derivedFrom":makeQuery(id+"F2.opPattern","COPY",BODY,{"derivedFrom":makeQuery(id+"F1.opRevolve","SWEPT_BODY",BODY,{"disambiguationData":[OSD([sQuery(id+"F0.wireOp",EDGE,"E1")])]}),"instanceName":"1"}),"instanceName":"1"}),"instanceName":"1"});
            var Q11;
            Q11=makeQuery(id+"F7.opPattern","COPY",BODY,{"derivedFrom":makeQuery(id+"F2.opPattern","COPY",BODY,{"derivedFrom":makeQuery(id+"F1.opRevolve","SWEPT_BODY",BODY,{"disambiguationData":[OSD([sQuery(id+"F0.wireOp",EDGE,"E1")])]}),"instanceName":"1"}),"instanceName":"1"});
            var Q12;
            Q12=makeQuery(id+"F7.opPattern","COPY",BODY,{"derivedFrom":makeQuery(id+"F1.opRevolve","SWEPT_BODY",BODY,{"disambiguationData":[OSD([sQuery(id+"F0.wireOp",EDGE,"E1")])]}),"instanceName":"1"});
            var Q13;
            Q13=makeQuery(id+"F6.opPattern","COPY",BODY,{"derivedFrom":makeQuery(id+"F1.opRevolve","SWEPT_BODY",BODY,{"disambiguationData":[OSD([sQuery(id+"F0.wireOp",EDGE,"E1")])]}),"instanceName":"1"});
            var Q14;
            Q14=makeQuery(id+"F5.opPattern","COPY",BODY,{"derivedFrom":makeQuery(id+"F2.opPattern","COPY",BODY,{"derivedFrom":makeQuery(id+"F1.opRevolve","SWEPT_BODY",BODY,{"disambiguationData":[OSD([sQuery(id+"F0.wireOp",EDGE,"E1")])]}),"instanceName":"1"}),"instanceName":"1"});
            var Q15;
            Q15=makeQuery(id+"F5.opPattern","COPY",BODY,{"derivedFrom":makeQuery(id+"F3.opPattern","COPY",BODY,{"derivedFrom":makeQuery(id+"F2.opPattern","COPY",BODY,{"derivedFrom":makeQuery(id+"F1.opRevolve","SWEPT_BODY",BODY,{"disambiguationData":[OSD([sQuery(id+"F0.wireOp",EDGE,"E1")])]}),"instanceName":"1"}),"instanceName":"1"}),"instanceName":"1"});
            var Q16;
            Q16=makeQuery(id+"F5.opPattern","COPY",BODY,{"derivedFrom":makeQuery(id+"F4.opPattern","COPY",BODY,{"derivedFrom":makeQuery(id+"F1.opRevolve","SWEPT_BODY",BODY,{"disambiguationData":[OSD([sQuery(id+"F0.wireOp",EDGE,"E1")])]}),"instanceName":"1"}),"instanceName":"1"});
            var Q17;
            Q17=makeQuery(id+"F5.opPattern","COPY",BODY,{"derivedFrom":makeQuery(id+"F4.opPattern","COPY",BODY,{"derivedFrom":makeQuery(id+"F2.opPattern","COPY",BODY,{"derivedFrom":makeQuery(id+"F1.opRevolve","SWEPT_BODY",BODY,{"disambiguationData":[OSD([sQuery(id+"F0.wireOp",EDGE,"E1")])]}),"instanceName":"1"}),"instanceName":"1"}),"instanceName":"1"});
            var Q18;
            Q18=makeQuery(id+"F5.opPattern","COPY",BODY,{"derivedFrom":makeQuery(id+"F4.opPattern","COPY",BODY,{"derivedFrom":makeQuery(id+"F3.opPattern","COPY",BODY,{"derivedFrom":makeQuery(id+"F2.opPattern","COPY",BODY,{"derivedFrom":makeQuery(id+"F1.opRevolve","SWEPT_BODY",BODY,{"disambiguationData":[OSD([sQuery(id+"F0.wireOp",EDGE,"E1")])]}),"instanceName":"1"}),"instanceName":"1"}),"instanceName":"1"}),"instanceName":"1"});
            var Q19;
            Q19=makeQuery(id+"F7.opPattern","COPY",BODY,{"derivedFrom":makeQuery(id+"F5.opPattern","COPY",BODY,{"derivedFrom":makeQuery(id+"F1.opRevolve","SWEPT_BODY",BODY,{"disambiguationData":[OSD([sQuery(id+"F0.wireOp",EDGE,"E1")])]}),"instanceName":"1"}),"instanceName":"1"});
            var Q20;
            Q20=makeQuery(id+"F6.opPattern","COPY",BODY,{"derivedFrom":makeQuery(id+"F2.opPattern","COPY",BODY,{"derivedFrom":makeQuery(id+"F1.opRevolve","SWEPT_BODY",BODY,{"disambiguationData":[OSD([sQuery(id+"F0.wireOp",EDGE,"E1")])]}),"instanceName":"1"}),"instanceName":"1"});
            var Q21;
            Q21=makeQuery(id+"F6.opPattern","COPY",BODY,{"derivedFrom":makeQuery(id+"F3.opPattern","COPY",BODY,{"derivedFrom":makeQuery(id+"F2.opPattern","COPY",BODY,{"derivedFrom":makeQuery(id+"F1.opRevolve","SWEPT_BODY",BODY,{"disambiguationData":[OSD([sQuery(id+"F0.wireOp",EDGE,"E1")])]}),"instanceName":"1"}),"instanceName":"1"}),"instanceName":"1"});
            var Q22;
            Q22=makeQuery(id+"F6.opPattern","COPY",BODY,{"derivedFrom":makeQuery(id+"F4.opPattern","COPY",BODY,{"derivedFrom":makeQuery(id+"F1.opRevolve","SWEPT_BODY",BODY,{"disambiguationData":[OSD([sQuery(id+"F0.wireOp",EDGE,"E1")])]}),"instanceName":"1"}),"instanceName":"1"});
            var Q23;
            Q23=makeQuery(id+"F6.opPattern","COPY",BODY,{"derivedFrom":makeQuery(id+"F4.opPattern","COPY",BODY,{"derivedFrom":makeQuery(id+"F2.opPattern","COPY",BODY,{"derivedFrom":makeQuery(id+"F1.opRevolve","SWEPT_BODY",BODY,{"disambiguationData":[OSD([sQuery(id+"F0.wireOp",EDGE,"E1")])]}),"instanceName":"1"}),"instanceName":"1"}),"instanceName":"1"});
            var Q24;
            Q24=makeQuery(id+"F6.opPattern","COPY",BODY,{"derivedFrom":makeQuery(id+"F4.opPattern","COPY",BODY,{"derivedFrom":makeQuery(id+"F3.opPattern","COPY",BODY,{"derivedFrom":makeQuery(id+"F2.opPattern","COPY",BODY,{"derivedFrom":makeQuery(id+"F1.opRevolve","SWEPT_BODY",BODY,{"disambiguationData":[OSD([sQuery(id+"F0.wireOp",EDGE,"E1")])]}),"instanceName":"1"}),"instanceName":"1"}),"instanceName":"1"}),"instanceName":"1"});
            var Q25;
            Q25=makeQuery(id+"F6.opPattern","COPY",BODY,{"derivedFrom":makeQuery(id+"F5.opPattern","COPY",BODY,{"derivedFrom":makeQuery(id+"F1.opRevolve","SWEPT_BODY",BODY,{"disambiguationData":[OSD([sQuery(id+"F0.wireOp",EDGE,"E1")])]}),"instanceName":"1"}),"instanceName":"1"});
            var Q26;
            Q26=makeQuery(id+"F6.opPattern","COPY",BODY,{"derivedFrom":makeQuery(id+"F5.opPattern","COPY",BODY,{"derivedFrom":makeQuery(id+"F2.opPattern","COPY",BODY,{"derivedFrom":makeQuery(id+"F1.opRevolve","SWEPT_BODY",BODY,{"disambiguationData":[OSD([sQuery(id+"F0.wireOp",EDGE,"E1")])]}),"instanceName":"1"}),"instanceName":"1"}),"instanceName":"1"});
            var Q27;
            Q27=makeQuery(id+"F6.opPattern","COPY",BODY,{"derivedFrom":makeQuery(id+"F5.opPattern","COPY",BODY,{"derivedFrom":makeQuery(id+"F3.opPattern","COPY",BODY,{"derivedFrom":makeQuery(id+"F2.opPattern","COPY",BODY,{"derivedFrom":makeQuery(id+"F1.opRevolve","SWEPT_BODY",BODY,{"disambiguationData":[OSD([sQuery(id+"F0.wireOp",EDGE,"E1")])]}),"instanceName":"1"}),"instanceName":"1"}),"instanceName":"1"}),"instanceName":"1"});
            var Q28;
            Q28=makeQuery(id+"F6.opPattern","COPY",BODY,{"derivedFrom":makeQuery(id+"F5.opPattern","COPY",BODY,{"derivedFrom":makeQuery(id+"F4.opPattern","COPY",BODY,{"derivedFrom":makeQuery(id+"F1.opRevolve","SWEPT_BODY",BODY,{"disambiguationData":[OSD([sQuery(id+"F0.wireOp",EDGE,"E1")])]}),"instanceName":"1"}),"instanceName":"1"}),"instanceName":"1"});
            var Q29;
            Q29=makeQuery(id+"F6.opPattern","COPY",BODY,{"derivedFrom":makeQuery(id+"F5.opPattern","COPY",BODY,{"derivedFrom":makeQuery(id+"F4.opPattern","COPY",BODY,{"derivedFrom":makeQuery(id+"F2.opPattern","COPY",BODY,{"derivedFrom":makeQuery(id+"F1.opRevolve","SWEPT_BODY",BODY,{"disambiguationData":[OSD([sQuery(id+"F0.wireOp",EDGE,"E1")])]}),"instanceName":"1"}),"instanceName":"1"}),"instanceName":"1"}),"instanceName":"1"});
            var Q30;
            Q30=makeQuery(id+"F6.opPattern","COPY",BODY,{"derivedFrom":makeQuery(id+"F5.opPattern","COPY",BODY,{"derivedFrom":makeQuery(id+"F4.opPattern","COPY",BODY,{"derivedFrom":makeQuery(id+"F3.opPattern","COPY",BODY,{"derivedFrom":makeQuery(id+"F2.opPattern","COPY",BODY,{"derivedFrom":makeQuery(id+"F1.opRevolve","SWEPT_BODY",BODY,{"disambiguationData":[OSD([sQuery(id+"F0.wireOp",EDGE,"E1")])]}),"instanceName":"1"}),"instanceName":"1"}),"instanceName":"1"}),"instanceName":"1"}),"instanceName":"1"});
            var Q31;
            Q31=makeQuery(id+"F7.opPattern","COPY",BODY,{"derivedFrom":makeQuery(id+"F5.opPattern","COPY",BODY,{"derivedFrom":makeQuery(id+"F2.opPattern","COPY",BODY,{"derivedFrom":makeQuery(id+"F1.opRevolve","SWEPT_BODY",BODY,{"disambiguationData":[OSD([sQuery(id+"F0.wireOp",EDGE,"E1")])]}),"instanceName":"1"}),"instanceName":"1"}),"instanceName":"1"});
            var Q32;
            Q32=makeQuery(id+"F7.opPattern","COPY",BODY,{"derivedFrom":makeQuery(id+"F5.opPattern","COPY",BODY,{"derivedFrom":makeQuery(id+"F3.opPattern","COPY",BODY,{"derivedFrom":makeQuery(id+"F2.opPattern","COPY",BODY,{"derivedFrom":makeQuery(id+"F1.opRevolve","SWEPT_BODY",BODY,{"disambiguationData":[OSD([sQuery(id+"F0.wireOp",EDGE,"E1")])]}),"instanceName":"1"}),"instanceName":"1"}),"instanceName":"1"}),"instanceName":"1"});
            var Q33;
            Q33=makeQuery(id+"F7.opPattern","COPY",BODY,{"derivedFrom":makeQuery(id+"F5.opPattern","COPY",BODY,{"derivedFrom":makeQuery(id+"F4.opPattern","COPY",BODY,{"derivedFrom":makeQuery(id+"F1.opRevolve","SWEPT_BODY",BODY,{"disambiguationData":[OSD([sQuery(id+"F0.wireOp",EDGE,"E1")])]}),"instanceName":"1"}),"instanceName":"1"}),"instanceName":"1"});
            var Q34;
            Q34=makeQuery(id+"F7.opPattern","COPY",BODY,{"derivedFrom":makeQuery(id+"F5.opPattern","COPY",BODY,{"derivedFrom":makeQuery(id+"F4.opPattern","COPY",BODY,{"derivedFrom":makeQuery(id+"F2.opPattern","COPY",BODY,{"derivedFrom":makeQuery(id+"F1.opRevolve","SWEPT_BODY",BODY,{"disambiguationData":[OSD([sQuery(id+"F0.wireOp",EDGE,"E1")])]}),"instanceName":"1"}),"instanceName":"1"}),"instanceName":"1"}),"instanceName":"1"});
            var Q35;
            Q35=makeQuery(id+"F7.opPattern","COPY",BODY,{"derivedFrom":makeQuery(id+"F5.opPattern","COPY",BODY,{"derivedFrom":makeQuery(id+"F4.opPattern","COPY",BODY,{"derivedFrom":makeQuery(id+"F3.opPattern","COPY",BODY,{"derivedFrom":makeQuery(id+"F2.opPattern","COPY",BODY,{"derivedFrom":makeQuery(id+"F1.opRevolve","SWEPT_BODY",BODY,{"disambiguationData":[OSD([sQuery(id+"F0.wireOp",EDGE,"E1")])]}),"instanceName":"1"}),"instanceName":"1"}),"instanceName":"1"}),"instanceName":"1"}),"instanceName":"1"});
            var Q36;
            Q36=makeQuery(id+"F7.opPattern","COPY",BODY,{"derivedFrom":makeQuery(id+"F6.opPattern","COPY",BODY,{"derivedFrom":makeQuery(id+"F1.opRevolve","SWEPT_BODY",BODY,{"disambiguationData":[OSD([sQuery(id+"F0.wireOp",EDGE,"E1")])]}),"instanceName":"1"}),"instanceName":"1"});
            var Q37;
            Q37=makeQuery(id+"F7.opPattern","COPY",BODY,{"derivedFrom":makeQuery(id+"F6.opPattern","COPY",BODY,{"derivedFrom":makeQuery(id+"F2.opPattern","COPY",BODY,{"derivedFrom":makeQuery(id+"F1.opRevolve","SWEPT_BODY",BODY,{"disambiguationData":[OSD([sQuery(id+"F0.wireOp",EDGE,"E1")])]}),"instanceName":"1"}),"instanceName":"1"}),"instanceName":"1"});
            var Q38;
            Q38=makeQuery(id+"F7.opPattern","COPY",BODY,{"derivedFrom":makeQuery(id+"F6.opPattern","COPY",BODY,{"derivedFrom":makeQuery(id+"F3.opPattern","COPY",BODY,{"derivedFrom":makeQuery(id+"F2.opPattern","COPY",BODY,{"derivedFrom":makeQuery(id+"F1.opRevolve","SWEPT_BODY",BODY,{"disambiguationData":[OSD([sQuery(id+"F0.wireOp",EDGE,"E1")])]}),"instanceName":"1"}),"instanceName":"1"}),"instanceName":"1"}),"instanceName":"1"});
            var Q39;
            Q39=makeQuery(id+"F7.opPattern","COPY",BODY,{"derivedFrom":makeQuery(id+"F6.opPattern","COPY",BODY,{"derivedFrom":makeQuery(id+"F4.opPattern","COPY",BODY,{"derivedFrom":makeQuery(id+"F1.opRevolve","SWEPT_BODY",BODY,{"disambiguationData":[OSD([sQuery(id+"F0.wireOp",EDGE,"E1")])]}),"instanceName":"1"}),"instanceName":"1"}),"instanceName":"1"});
            var Q40;
            Q40=makeQuery(id+"F7.opPattern","COPY",BODY,{"derivedFrom":makeQuery(id+"F6.opPattern","COPY",BODY,{"derivedFrom":makeQuery(id+"F4.opPattern","COPY",BODY,{"derivedFrom":makeQuery(id+"F2.opPattern","COPY",BODY,{"derivedFrom":makeQuery(id+"F1.opRevolve","SWEPT_BODY",BODY,{"disambiguationData":[OSD([sQuery(id+"F0.wireOp",EDGE,"E1")])]}),"instanceName":"1"}),"instanceName":"1"}),"instanceName":"1"}),"instanceName":"1"});
            var Q41;
            Q41=makeQuery(id+"F7.opPattern","COPY",BODY,{"derivedFrom":makeQuery(id+"F6.opPattern","COPY",BODY,{"derivedFrom":makeQuery(id+"F4.opPattern","COPY",BODY,{"derivedFrom":makeQuery(id+"F3.opPattern","COPY",BODY,{"derivedFrom":makeQuery(id+"F2.opPattern","COPY",BODY,{"derivedFrom":makeQuery(id+"F1.opRevolve","SWEPT_BODY",BODY,{"disambiguationData":[OSD([sQuery(id+"F0.wireOp",EDGE,"E1")])]}),"instanceName":"1"}),"instanceName":"1"}),"instanceName":"1"}),"instanceName":"1"}),"instanceName":"1"});
            var Q42;
            Q42=makeQuery(id+"F7.opPattern","COPY",BODY,{"derivedFrom":makeQuery(id+"F6.opPattern","COPY",BODY,{"derivedFrom":makeQuery(id+"F5.opPattern","COPY",BODY,{"derivedFrom":makeQuery(id+"F1.opRevolve","SWEPT_BODY",BODY,{"disambiguationData":[OSD([sQuery(id+"F0.wireOp",EDGE,"E1")])]}),"instanceName":"1"}),"instanceName":"1"}),"instanceName":"1"});
            var Q43;
            Q43=makeQuery(id+"F7.opPattern","COPY",BODY,{"derivedFrom":makeQuery(id+"F6.opPattern","COPY",BODY,{"derivedFrom":makeQuery(id+"F5.opPattern","COPY",BODY,{"derivedFrom":makeQuery(id+"F2.opPattern","COPY",BODY,{"derivedFrom":makeQuery(id+"F1.opRevolve","SWEPT_BODY",BODY,{"disambiguationData":[OSD([sQuery(id+"F0.wireOp",EDGE,"E1")])]}),"instanceName":"1"}),"instanceName":"1"}),"instanceName":"1"}),"instanceName":"1"});
            var Q44;
            Q44=makeQuery(id+"F7.opPattern","COPY",BODY,{"derivedFrom":makeQuery(id+"F6.opPattern","COPY",BODY,{"derivedFrom":makeQuery(id+"F5.opPattern","COPY",BODY,{"derivedFrom":makeQuery(id+"F3.opPattern","COPY",BODY,{"derivedFrom":makeQuery(id+"F2.opPattern","COPY",BODY,{"derivedFrom":makeQuery(id+"F1.opRevolve","SWEPT_BODY",BODY,{"disambiguationData":[OSD([sQuery(id+"F0.wireOp",EDGE,"E1")])]}),"instanceName":"1"}),"instanceName":"1"}),"instanceName":"1"}),"instanceName":"1"}),"instanceName":"1"});
            var Q45;
            Q45=makeQuery(id+"F7.opPattern","COPY",BODY,{"derivedFrom":makeQuery(id+"F6.opPattern","COPY",BODY,{"derivedFrom":makeQuery(id+"F5.opPattern","COPY",BODY,{"derivedFrom":makeQuery(id+"F4.opPattern","COPY",BODY,{"derivedFrom":makeQuery(id+"F1.opRevolve","SWEPT_BODY",BODY,{"disambiguationData":[OSD([sQuery(id+"F0.wireOp",EDGE,"E1")])]}),"instanceName":"1"}),"instanceName":"1"}),"instanceName":"1"}),"instanceName":"1"});
            var Q46;
            Q46=makeQuery(id+"F7.opPattern","COPY",BODY,{"derivedFrom":makeQuery(id+"F6.opPattern","COPY",BODY,{"derivedFrom":makeQuery(id+"F5.opPattern","COPY",BODY,{"derivedFrom":makeQuery(id+"F4.opPattern","COPY",BODY,{"derivedFrom":makeQuery(id+"F2.opPattern","COPY",BODY,{"derivedFrom":makeQuery(id+"F1.opRevolve","SWEPT_BODY",BODY,{"disambiguationData":[OSD([sQuery(id+"F0.wireOp",EDGE,"E1")])]}),"instanceName":"1"}),"instanceName":"1"}),"instanceName":"1"}),"instanceName":"1"}),"instanceName":"1"});
            var Q47;
            Q47=makeQuery(id+"F7.opPattern","COPY",BODY,{"derivedFrom":makeQuery(id+"F6.opPattern","COPY",BODY,{"derivedFrom":makeQuery(id+"F5.opPattern","COPY",BODY,{"derivedFrom":makeQuery(id+"F4.opPattern","COPY",BODY,{"derivedFrom":makeQuery(id+"F3.opPattern","COPY",BODY,{"derivedFrom":makeQuery(id+"F2.opPattern","COPY",BODY,{"derivedFrom":makeQuery(id+"F1.opRevolve","SWEPT_BODY",BODY,{"disambiguationData":[OSD([sQuery(id+"F0.wireOp",EDGE,"E1")])]}),"instanceName":"1"}),"instanceName":"1"}),"instanceName":"1"}),"instanceName":"1"}),"instanceName":"1"}),"instanceName":"1"});
            var Q48;
            Q48=makeQuery(id+"F8.opPattern","COPY",BODY,{"derivedFrom":makeQuery(id+"F5.opPattern","COPY",BODY,{"derivedFrom":makeQuery(id+"F1.opRevolve","SWEPT_BODY",BODY,{"disambiguationData":[OSD([sQuery(id+"F0.wireOp",EDGE,"E1")])]}),"instanceName":"1"}),"instanceName":"1"});
            var Q49;
            Q49=makeQuery(id+"F8.opPattern","COPY",BODY,{"derivedFrom":makeQuery(id+"F4.opPattern","COPY",BODY,{"derivedFrom":makeQuery(id+"F3.opPattern","COPY",BODY,{"derivedFrom":makeQuery(id+"F2.opPattern","COPY",BODY,{"derivedFrom":makeQuery(id+"F1.opRevolve","SWEPT_BODY",BODY,{"disambiguationData":[OSD([sQuery(id+"F0.wireOp",EDGE,"E1")])]}),"instanceName":"1"}),"instanceName":"1"}),"instanceName":"1"}),"instanceName":"1"});
            var Q50;
            Q50=makeQuery(id+"F8.opPattern","COPY",BODY,{"derivedFrom":makeQuery(id+"F4.opPattern","COPY",BODY,{"derivedFrom":makeQuery(id+"F2.opPattern","COPY",BODY,{"derivedFrom":makeQuery(id+"F1.opRevolve","SWEPT_BODY",BODY,{"disambiguationData":[OSD([sQuery(id+"F0.wireOp",EDGE,"E1")])]}),"instanceName":"1"}),"instanceName":"1"}),"instanceName":"1"});
            var Q51;
            Q51=makeQuery(id+"F8.opPattern","COPY",BODY,{"derivedFrom":makeQuery(id+"F4.opPattern","COPY",BODY,{"derivedFrom":makeQuery(id+"F1.opRevolve","SWEPT_BODY",BODY,{"disambiguationData":[OSD([sQuery(id+"F0.wireOp",EDGE,"E1")])]}),"instanceName":"1"}),"instanceName":"1"});
            var Q52;
            Q52=makeQuery(id+"F8.opPattern","COPY",BODY,{"derivedFrom":makeQuery(id+"F3.opPattern","COPY",BODY,{"derivedFrom":makeQuery(id+"F2.opPattern","COPY",BODY,{"derivedFrom":makeQuery(id+"F1.opRevolve","SWEPT_BODY",BODY,{"disambiguationData":[OSD([sQuery(id+"F0.wireOp",EDGE,"E1")])]}),"instanceName":"1"}),"instanceName":"1"}),"instanceName":"1"});
            var Q53;
            Q53=makeQuery(id+"F8.opPattern","COPY",BODY,{"derivedFrom":makeQuery(id+"F2.opPattern","COPY",BODY,{"derivedFrom":makeQuery(id+"F1.opRevolve","SWEPT_BODY",BODY,{"disambiguationData":[OSD([sQuery(id+"F0.wireOp",EDGE,"E1")])]}),"instanceName":"1"}),"instanceName":"1"});
            var Q54;
            Q54=makeQuery(id+"F8.opPattern","COPY",BODY,{"derivedFrom":makeQuery(id+"F1.opRevolve","SWEPT_BODY",BODY,{"disambiguationData":[OSD([sQuery(id+"F0.wireOp",EDGE,"E1")])]}),"instanceName":"1"});
            var Q55;
            Q55=makeQuery(id+"F8.opPattern","COPY",BODY,{"derivedFrom":makeQuery(id+"F5.opPattern","COPY",BODY,{"derivedFrom":makeQuery(id+"F2.opPattern","COPY",BODY,{"derivedFrom":makeQuery(id+"F1.opRevolve","SWEPT_BODY",BODY,{"disambiguationData":[OSD([sQuery(id+"F0.wireOp",EDGE,"E1")])]}),"instanceName":"1"}),"instanceName":"1"}),"instanceName":"1"});
            var Q56;
            Q56=makeQuery(id+"F8.opPattern","COPY",BODY,{"derivedFrom":makeQuery(id+"F5.opPattern","COPY",BODY,{"derivedFrom":makeQuery(id+"F3.opPattern","COPY",BODY,{"derivedFrom":makeQuery(id+"F2.opPattern","COPY",BODY,{"derivedFrom":makeQuery(id+"F1.opRevolve","SWEPT_BODY",BODY,{"disambiguationData":[OSD([sQuery(id+"F0.wireOp",EDGE,"E1")])]}),"instanceName":"1"}),"instanceName":"1"}),"instanceName":"1"}),"instanceName":"1"});
            var Q57;
            Q57=makeQuery(id+"F8.opPattern","COPY",BODY,{"derivedFrom":makeQuery(id+"F5.opPattern","COPY",BODY,{"derivedFrom":makeQuery(id+"F4.opPattern","COPY",BODY,{"derivedFrom":makeQuery(id+"F1.opRevolve","SWEPT_BODY",BODY,{"disambiguationData":[OSD([sQuery(id+"F0.wireOp",EDGE,"E1")])]}),"instanceName":"1"}),"instanceName":"1"}),"instanceName":"1"});
            var Q58;
            Q58=makeQuery(id+"F8.opPattern","COPY",BODY,{"derivedFrom":makeQuery(id+"F5.opPattern","COPY",BODY,{"derivedFrom":makeQuery(id+"F4.opPattern","COPY",BODY,{"derivedFrom":makeQuery(id+"F2.opPattern","COPY",BODY,{"derivedFrom":makeQuery(id+"F1.opRevolve","SWEPT_BODY",BODY,{"disambiguationData":[OSD([sQuery(id+"F0.wireOp",EDGE,"E1")])]}),"instanceName":"1"}),"instanceName":"1"}),"instanceName":"1"}),"instanceName":"1"});
            var Q59;
            Q59=makeQuery(id+"F8.opPattern","COPY",BODY,{"derivedFrom":makeQuery(id+"F5.opPattern","COPY",BODY,{"derivedFrom":makeQuery(id+"F4.opPattern","COPY",BODY,{"derivedFrom":makeQuery(id+"F3.opPattern","COPY",BODY,{"derivedFrom":makeQuery(id+"F2.opPattern","COPY",BODY,{"derivedFrom":makeQuery(id+"F1.opRevolve","SWEPT_BODY",BODY,{"disambiguationData":[OSD([sQuery(id+"F0.wireOp",EDGE,"E1")])]}),"instanceName":"1"}),"instanceName":"1"}),"instanceName":"1"}),"instanceName":"1"}),"instanceName":"1"});
            var Q60;
            Q60=makeQuery(id+"F8.opPattern","COPY",BODY,{"derivedFrom":makeQuery(id+"F6.opPattern","COPY",BODY,{"derivedFrom":makeQuery(id+"F1.opRevolve","SWEPT_BODY",BODY,{"disambiguationData":[OSD([sQuery(id+"F0.wireOp",EDGE,"E1")])]}),"instanceName":"1"}),"instanceName":"1"});
            var Q61;
            Q61=makeQuery(id+"F8.opPattern","COPY",BODY,{"derivedFrom":makeQuery(id+"F6.opPattern","COPY",BODY,{"derivedFrom":makeQuery(id+"F2.opPattern","COPY",BODY,{"derivedFrom":makeQuery(id+"F1.opRevolve","SWEPT_BODY",BODY,{"disambiguationData":[OSD([sQuery(id+"F0.wireOp",EDGE,"E1")])]}),"instanceName":"1"}),"instanceName":"1"}),"instanceName":"1"});
            var Q62;
            Q62=makeQuery(id+"F8.opPattern","COPY",BODY,{"derivedFrom":makeQuery(id+"F6.opPattern","COPY",BODY,{"derivedFrom":makeQuery(id+"F3.opPattern","COPY",BODY,{"derivedFrom":makeQuery(id+"F2.opPattern","COPY",BODY,{"derivedFrom":makeQuery(id+"F1.opRevolve","SWEPT_BODY",BODY,{"disambiguationData":[OSD([sQuery(id+"F0.wireOp",EDGE,"E1")])]}),"instanceName":"1"}),"instanceName":"1"}),"instanceName":"1"}),"instanceName":"1"});
            var Q63;
            Q63=makeQuery(id+"F8.opPattern","COPY",BODY,{"derivedFrom":makeQuery(id+"F6.opPattern","COPY",BODY,{"derivedFrom":makeQuery(id+"F4.opPattern","COPY",BODY,{"derivedFrom":makeQuery(id+"F1.opRevolve","SWEPT_BODY",BODY,{"disambiguationData":[OSD([sQuery(id+"F0.wireOp",EDGE,"E1")])]}),"instanceName":"1"}),"instanceName":"1"}),"instanceName":"1"});
            var Q64;
            Q64=makeQuery(id+"F8.opPattern","COPY",BODY,{"derivedFrom":makeQuery(id+"F6.opPattern","COPY",BODY,{"derivedFrom":makeQuery(id+"F4.opPattern","COPY",BODY,{"derivedFrom":makeQuery(id+"F2.opPattern","COPY",BODY,{"derivedFrom":makeQuery(id+"F1.opRevolve","SWEPT_BODY",BODY,{"disambiguationData":[OSD([sQuery(id+"F0.wireOp",EDGE,"E1")])]}),"instanceName":"1"}),"instanceName":"1"}),"instanceName":"1"}),"instanceName":"1"});
            var Q65;
            Q65=makeQuery(id+"F8.opPattern","COPY",BODY,{"derivedFrom":makeQuery(id+"F6.opPattern","COPY",BODY,{"derivedFrom":makeQuery(id+"F4.opPattern","COPY",BODY,{"derivedFrom":makeQuery(id+"F3.opPattern","COPY",BODY,{"derivedFrom":makeQuery(id+"F2.opPattern","COPY",BODY,{"derivedFrom":makeQuery(id+"F1.opRevolve","SWEPT_BODY",BODY,{"disambiguationData":[OSD([sQuery(id+"F0.wireOp",EDGE,"E1")])]}),"instanceName":"1"}),"instanceName":"1"}),"instanceName":"1"}),"instanceName":"1"}),"instanceName":"1"});
            var Q66;
            Q66=makeQuery(id+"F8.opPattern","COPY",BODY,{"derivedFrom":makeQuery(id+"F6.opPattern","COPY",BODY,{"derivedFrom":makeQuery(id+"F5.opPattern","COPY",BODY,{"derivedFrom":makeQuery(id+"F1.opRevolve","SWEPT_BODY",BODY,{"disambiguationData":[OSD([sQuery(id+"F0.wireOp",EDGE,"E1")])]}),"instanceName":"1"}),"instanceName":"1"}),"instanceName":"1"});
            var Q67;
            Q67=makeQuery(id+"F8.opPattern","COPY",BODY,{"derivedFrom":makeQuery(id+"F6.opPattern","COPY",BODY,{"derivedFrom":makeQuery(id+"F5.opPattern","COPY",BODY,{"derivedFrom":makeQuery(id+"F2.opPattern","COPY",BODY,{"derivedFrom":makeQuery(id+"F1.opRevolve","SWEPT_BODY",BODY,{"disambiguationData":[OSD([sQuery(id+"F0.wireOp",EDGE,"E1")])]}),"instanceName":"1"}),"instanceName":"1"}),"instanceName":"1"}),"instanceName":"1"});
            var Q68;
            Q68=makeQuery(id+"F8.opPattern","COPY",BODY,{"derivedFrom":makeQuery(id+"F6.opPattern","COPY",BODY,{"derivedFrom":makeQuery(id+"F5.opPattern","COPY",BODY,{"derivedFrom":makeQuery(id+"F3.opPattern","COPY",BODY,{"derivedFrom":makeQuery(id+"F2.opPattern","COPY",BODY,{"derivedFrom":makeQuery(id+"F1.opRevolve","SWEPT_BODY",BODY,{"disambiguationData":[OSD([sQuery(id+"F0.wireOp",EDGE,"E1")])]}),"instanceName":"1"}),"instanceName":"1"}),"instanceName":"1"}),"instanceName":"1"}),"instanceName":"1"});
            var Q69;
            Q69=makeQuery(id+"F8.opPattern","COPY",BODY,{"derivedFrom":makeQuery(id+"F6.opPattern","COPY",BODY,{"derivedFrom":makeQuery(id+"F5.opPattern","COPY",BODY,{"derivedFrom":makeQuery(id+"F4.opPattern","COPY",BODY,{"derivedFrom":makeQuery(id+"F1.opRevolve","SWEPT_BODY",BODY,{"disambiguationData":[OSD([sQuery(id+"F0.wireOp",EDGE,"E1")])]}),"instanceName":"1"}),"instanceName":"1"}),"instanceName":"1"}),"instanceName":"1"});
            var Q70;
            Q70=makeQuery(id+"F8.opPattern","COPY",BODY,{"derivedFrom":makeQuery(id+"F6.opPattern","COPY",BODY,{"derivedFrom":makeQuery(id+"F5.opPattern","COPY",BODY,{"derivedFrom":makeQuery(id+"F4.opPattern","COPY",BODY,{"derivedFrom":makeQuery(id+"F2.opPattern","COPY",BODY,{"derivedFrom":makeQuery(id+"F1.opRevolve","SWEPT_BODY",BODY,{"disambiguationData":[OSD([sQuery(id+"F0.wireOp",EDGE,"E1")])]}),"instanceName":"1"}),"instanceName":"1"}),"instanceName":"1"}),"instanceName":"1"}),"instanceName":"1"});
            var Q71;
            Q71=makeQuery(id+"F8.opPattern","COPY",BODY,{"derivedFrom":makeQuery(id+"F6.opPattern","COPY",BODY,{"derivedFrom":makeQuery(id+"F5.opPattern","COPY",BODY,{"derivedFrom":makeQuery(id+"F4.opPattern","COPY",BODY,{"derivedFrom":makeQuery(id+"F3.opPattern","COPY",BODY,{"derivedFrom":makeQuery(id+"F2.opPattern","COPY",BODY,{"derivedFrom":makeQuery(id+"F1.opRevolve","SWEPT_BODY",BODY,{"disambiguationData":[OSD([sQuery(id+"F0.wireOp",EDGE,"E1")])]}),"instanceName":"1"}),"instanceName":"1"}),"instanceName":"1"}),"instanceName":"1"}),"instanceName":"1"}),"instanceName":"1"});
            var Q72;
            Q72=makeQuery(id+"F8.opPattern","COPY",BODY,{"derivedFrom":makeQuery(id+"F7.opPattern","COPY",BODY,{"derivedFrom":makeQuery(id+"F1.opRevolve","SWEPT_BODY",BODY,{"disambiguationData":[OSD([sQuery(id+"F0.wireOp",EDGE,"E1")])]}),"instanceName":"1"}),"instanceName":"1"});
            var Q73;
            Q73=makeQuery(id+"F8.opPattern","COPY",BODY,{"derivedFrom":makeQuery(id+"F7.opPattern","COPY",BODY,{"derivedFrom":makeQuery(id+"F2.opPattern","COPY",BODY,{"derivedFrom":makeQuery(id+"F1.opRevolve","SWEPT_BODY",BODY,{"disambiguationData":[OSD([sQuery(id+"F0.wireOp",EDGE,"E1")])]}),"instanceName":"1"}),"instanceName":"1"}),"instanceName":"1"});
            var Q74;
            Q74=makeQuery(id+"F8.opPattern","COPY",BODY,{"derivedFrom":makeQuery(id+"F7.opPattern","COPY",BODY,{"derivedFrom":makeQuery(id+"F3.opPattern","COPY",BODY,{"derivedFrom":makeQuery(id+"F2.opPattern","COPY",BODY,{"derivedFrom":makeQuery(id+"F1.opRevolve","SWEPT_BODY",BODY,{"disambiguationData":[OSD([sQuery(id+"F0.wireOp",EDGE,"E1")])]}),"instanceName":"1"}),"instanceName":"1"}),"instanceName":"1"}),"instanceName":"1"});
            var Q75;
            Q75=makeQuery(id+"F8.opPattern","COPY",BODY,{"derivedFrom":makeQuery(id+"F7.opPattern","COPY",BODY,{"derivedFrom":makeQuery(id+"F4.opPattern","COPY",BODY,{"derivedFrom":makeQuery(id+"F1.opRevolve","SWEPT_BODY",BODY,{"disambiguationData":[OSD([sQuery(id+"F0.wireOp",EDGE,"E1")])]}),"instanceName":"1"}),"instanceName":"1"}),"instanceName":"1"});
            var Q76;
            Q76=makeQuery(id+"F8.opPattern","COPY",BODY,{"derivedFrom":makeQuery(id+"F7.opPattern","COPY",BODY,{"derivedFrom":makeQuery(id+"F4.opPattern","COPY",BODY,{"derivedFrom":makeQuery(id+"F2.opPattern","COPY",BODY,{"derivedFrom":makeQuery(id+"F1.opRevolve","SWEPT_BODY",BODY,{"disambiguationData":[OSD([sQuery(id+"F0.wireOp",EDGE,"E1")])]}),"instanceName":"1"}),"instanceName":"1"}),"instanceName":"1"}),"instanceName":"1"});
            var Q77;
            Q77=makeQuery(id+"F8.opPattern","COPY",BODY,{"derivedFrom":makeQuery(id+"F7.opPattern","COPY",BODY,{"derivedFrom":makeQuery(id+"F4.opPattern","COPY",BODY,{"derivedFrom":makeQuery(id+"F3.opPattern","COPY",BODY,{"derivedFrom":makeQuery(id+"F2.opPattern","COPY",BODY,{"derivedFrom":makeQuery(id+"F1.opRevolve","SWEPT_BODY",BODY,{"disambiguationData":[OSD([sQuery(id+"F0.wireOp",EDGE,"E1")])]}),"instanceName":"1"}),"instanceName":"1"}),"instanceName":"1"}),"instanceName":"1"}),"instanceName":"1"});
            var Q78;
            Q78=makeQuery(id+"F8.opPattern","COPY",BODY,{"derivedFrom":makeQuery(id+"F7.opPattern","COPY",BODY,{"derivedFrom":makeQuery(id+"F5.opPattern","COPY",BODY,{"derivedFrom":makeQuery(id+"F1.opRevolve","SWEPT_BODY",BODY,{"disambiguationData":[OSD([sQuery(id+"F0.wireOp",EDGE,"E1")])]}),"instanceName":"1"}),"instanceName":"1"}),"instanceName":"1"});
            var Q79;
            Q79=makeQuery(id+"F8.opPattern","COPY",BODY,{"derivedFrom":makeQuery(id+"F7.opPattern","COPY",BODY,{"derivedFrom":makeQuery(id+"F5.opPattern","COPY",BODY,{"derivedFrom":makeQuery(id+"F2.opPattern","COPY",BODY,{"derivedFrom":makeQuery(id+"F1.opRevolve","SWEPT_BODY",BODY,{"disambiguationData":[OSD([sQuery(id+"F0.wireOp",EDGE,"E1")])]}),"instanceName":"1"}),"instanceName":"1"}),"instanceName":"1"}),"instanceName":"1"});
            var Q80;
            Q80=makeQuery(id+"F8.opPattern","COPY",BODY,{"derivedFrom":makeQuery(id+"F7.opPattern","COPY",BODY,{"derivedFrom":makeQuery(id+"F5.opPattern","COPY",BODY,{"derivedFrom":makeQuery(id+"F3.opPattern","COPY",BODY,{"derivedFrom":makeQuery(id+"F2.opPattern","COPY",BODY,{"derivedFrom":makeQuery(id+"F1.opRevolve","SWEPT_BODY",BODY,{"disambiguationData":[OSD([sQuery(id+"F0.wireOp",EDGE,"E1")])]}),"instanceName":"1"}),"instanceName":"1"}),"instanceName":"1"}),"instanceName":"1"}),"instanceName":"1"});
            var Q81;
            Q81=makeQuery(id+"F8.opPattern","COPY",BODY,{"derivedFrom":makeQuery(id+"F7.opPattern","COPY",BODY,{"derivedFrom":makeQuery(id+"F5.opPattern","COPY",BODY,{"derivedFrom":makeQuery(id+"F4.opPattern","COPY",BODY,{"derivedFrom":makeQuery(id+"F1.opRevolve","SWEPT_BODY",BODY,{"disambiguationData":[OSD([sQuery(id+"F0.wireOp",EDGE,"E1")])]}),"instanceName":"1"}),"instanceName":"1"}),"instanceName":"1"}),"instanceName":"1"});
            var Q82;
            Q82=makeQuery(id+"F8.opPattern","COPY",BODY,{"derivedFrom":makeQuery(id+"F7.opPattern","COPY",BODY,{"derivedFrom":makeQuery(id+"F5.opPattern","COPY",BODY,{"derivedFrom":makeQuery(id+"F4.opPattern","COPY",BODY,{"derivedFrom":makeQuery(id+"F2.opPattern","COPY",BODY,{"derivedFrom":makeQuery(id+"F1.opRevolve","SWEPT_BODY",BODY,{"disambiguationData":[OSD([sQuery(id+"F0.wireOp",EDGE,"E1")])]}),"instanceName":"1"}),"instanceName":"1"}),"instanceName":"1"}),"instanceName":"1"}),"instanceName":"1"});
            var Q83;
            Q83=makeQuery(id+"F8.opPattern","COPY",BODY,{"derivedFrom":makeQuery(id+"F7.opPattern","COPY",BODY,{"derivedFrom":makeQuery(id+"F5.opPattern","COPY",BODY,{"derivedFrom":makeQuery(id+"F4.opPattern","COPY",BODY,{"derivedFrom":makeQuery(id+"F3.opPattern","COPY",BODY,{"derivedFrom":makeQuery(id+"F2.opPattern","COPY",BODY,{"derivedFrom":makeQuery(id+"F1.opRevolve","SWEPT_BODY",BODY,{"disambiguationData":[OSD([sQuery(id+"F0.wireOp",EDGE,"E1")])]}),"instanceName":"1"}),"instanceName":"1"}),"instanceName":"1"}),"instanceName":"1"}),"instanceName":"1"}),"instanceName":"1"});
            var Q84;
            Q84=makeQuery(id+"F8.opPattern","COPY",BODY,{"derivedFrom":makeQuery(id+"F7.opPattern","COPY",BODY,{"derivedFrom":makeQuery(id+"F6.opPattern","COPY",BODY,{"derivedFrom":makeQuery(id+"F1.opRevolve","SWEPT_BODY",BODY,{"disambiguationData":[OSD([sQuery(id+"F0.wireOp",EDGE,"E1")])]}),"instanceName":"1"}),"instanceName":"1"}),"instanceName":"1"});
            var Q85;
            Q85=makeQuery(id+"F8.opPattern","COPY",BODY,{"derivedFrom":makeQuery(id+"F7.opPattern","COPY",BODY,{"derivedFrom":makeQuery(id+"F6.opPattern","COPY",BODY,{"derivedFrom":makeQuery(id+"F2.opPattern","COPY",BODY,{"derivedFrom":makeQuery(id+"F1.opRevolve","SWEPT_BODY",BODY,{"disambiguationData":[OSD([sQuery(id+"F0.wireOp",EDGE,"E1")])]}),"instanceName":"1"}),"instanceName":"1"}),"instanceName":"1"}),"instanceName":"1"});
            var Q86;
            Q86=makeQuery(id+"F8.opPattern","COPY",BODY,{"derivedFrom":makeQuery(id+"F7.opPattern","COPY",BODY,{"derivedFrom":makeQuery(id+"F6.opPattern","COPY",BODY,{"derivedFrom":makeQuery(id+"F3.opPattern","COPY",BODY,{"derivedFrom":makeQuery(id+"F2.opPattern","COPY",BODY,{"derivedFrom":makeQuery(id+"F1.opRevolve","SWEPT_BODY",BODY,{"disambiguationData":[OSD([sQuery(id+"F0.wireOp",EDGE,"E1")])]}),"instanceName":"1"}),"instanceName":"1"}),"instanceName":"1"}),"instanceName":"1"}),"instanceName":"1"});
            var Q87;
            Q87=makeQuery(id+"F8.opPattern","COPY",BODY,{"derivedFrom":makeQuery(id+"F7.opPattern","COPY",BODY,{"derivedFrom":makeQuery(id+"F6.opPattern","COPY",BODY,{"derivedFrom":makeQuery(id+"F4.opPattern","COPY",BODY,{"derivedFrom":makeQuery(id+"F1.opRevolve","SWEPT_BODY",BODY,{"disambiguationData":[OSD([sQuery(id+"F0.wireOp",EDGE,"E1")])]}),"instanceName":"1"}),"instanceName":"1"}),"instanceName":"1"}),"instanceName":"1"});
            var Q88;
            Q88=makeQuery(id+"F8.opPattern","COPY",BODY,{"derivedFrom":makeQuery(id+"F7.opPattern","COPY",BODY,{"derivedFrom":makeQuery(id+"F6.opPattern","COPY",BODY,{"derivedFrom":makeQuery(id+"F4.opPattern","COPY",BODY,{"derivedFrom":makeQuery(id+"F2.opPattern","COPY",BODY,{"derivedFrom":makeQuery(id+"F1.opRevolve","SWEPT_BODY",BODY,{"disambiguationData":[OSD([sQuery(id+"F0.wireOp",EDGE,"E1")])]}),"instanceName":"1"}),"instanceName":"1"}),"instanceName":"1"}),"instanceName":"1"}),"instanceName":"1"});
            var Q89;
            Q89=makeQuery(id+"F8.opPattern","COPY",BODY,{"derivedFrom":makeQuery(id+"F7.opPattern","COPY",BODY,{"derivedFrom":makeQuery(id+"F6.opPattern","COPY",BODY,{"derivedFrom":makeQuery(id+"F4.opPattern","COPY",BODY,{"derivedFrom":makeQuery(id+"F3.opPattern","COPY",BODY,{"derivedFrom":makeQuery(id+"F2.opPattern","COPY",BODY,{"derivedFrom":makeQuery(id+"F1.opRevolve","SWEPT_BODY",BODY,{"disambiguationData":[OSD([sQuery(id+"F0.wireOp",EDGE,"E1")])]}),"instanceName":"1"}),"instanceName":"1"}),"instanceName":"1"}),"instanceName":"1"}),"instanceName":"1"}),"instanceName":"1"});
            var Q90;
            Q90=makeQuery(id+"F8.opPattern","COPY",BODY,{"derivedFrom":makeQuery(id+"F7.opPattern","COPY",BODY,{"derivedFrom":makeQuery(id+"F6.opPattern","COPY",BODY,{"derivedFrom":makeQuery(id+"F5.opPattern","COPY",BODY,{"derivedFrom":makeQuery(id+"F1.opRevolve","SWEPT_BODY",BODY,{"disambiguationData":[OSD([sQuery(id+"F0.wireOp",EDGE,"E1")])]}),"instanceName":"1"}),"instanceName":"1"}),"instanceName":"1"}),"instanceName":"1"});
            var Q91;
            Q91=makeQuery(id+"F8.opPattern","COPY",BODY,{"derivedFrom":makeQuery(id+"F7.opPattern","COPY",BODY,{"derivedFrom":makeQuery(id+"F6.opPattern","COPY",BODY,{"derivedFrom":makeQuery(id+"F5.opPattern","COPY",BODY,{"derivedFrom":makeQuery(id+"F2.opPattern","COPY",BODY,{"derivedFrom":makeQuery(id+"F1.opRevolve","SWEPT_BODY",BODY,{"disambiguationData":[OSD([sQuery(id+"F0.wireOp",EDGE,"E1")])]}),"instanceName":"1"}),"instanceName":"1"}),"instanceName":"1"}),"instanceName":"1"}),"instanceName":"1"});
            var Q92;
            Q92=makeQuery(id+"F8.opPattern","COPY",BODY,{"derivedFrom":makeQuery(id+"F7.opPattern","COPY",BODY,{"derivedFrom":makeQuery(id+"F6.opPattern","COPY",BODY,{"derivedFrom":makeQuery(id+"F5.opPattern","COPY",BODY,{"derivedFrom":makeQuery(id+"F3.opPattern","COPY",BODY,{"derivedFrom":makeQuery(id+"F2.opPattern","COPY",BODY,{"derivedFrom":makeQuery(id+"F1.opRevolve","SWEPT_BODY",BODY,{"disambiguationData":[OSD([sQuery(id+"F0.wireOp",EDGE,"E1")])]}),"instanceName":"1"}),"instanceName":"1"}),"instanceName":"1"}),"instanceName":"1"}),"instanceName":"1"}),"instanceName":"1"});
            var Q93;
            Q93=makeQuery(id+"F8.opPattern","COPY",BODY,{"derivedFrom":makeQuery(id+"F7.opPattern","COPY",BODY,{"derivedFrom":makeQuery(id+"F6.opPattern","COPY",BODY,{"derivedFrom":makeQuery(id+"F5.opPattern","COPY",BODY,{"derivedFrom":makeQuery(id+"F4.opPattern","COPY",BODY,{"derivedFrom":makeQuery(id+"F1.opRevolve","SWEPT_BODY",BODY,{"disambiguationData":[OSD([sQuery(id+"F0.wireOp",EDGE,"E1")])]}),"instanceName":"1"}),"instanceName":"1"}),"instanceName":"1"}),"instanceName":"1"}),"instanceName":"1"});
            var Q94;
            Q94=makeQuery(id+"F8.opPattern","COPY",BODY,{"derivedFrom":makeQuery(id+"F7.opPattern","COPY",BODY,{"derivedFrom":makeQuery(id+"F6.opPattern","COPY",BODY,{"derivedFrom":makeQuery(id+"F5.opPattern","COPY",BODY,{"derivedFrom":makeQuery(id+"F4.opPattern","COPY",BODY,{"derivedFrom":makeQuery(id+"F2.opPattern","COPY",BODY,{"derivedFrom":makeQuery(id+"F1.opRevolve","SWEPT_BODY",BODY,{"disambiguationData":[OSD([sQuery(id+"F0.wireOp",EDGE,"E1")])]}),"instanceName":"1"}),"instanceName":"1"}),"instanceName":"1"}),"instanceName":"1"}),"instanceName":"1"}),"instanceName":"1"});
            var Q95;
            Q95=makeQuery(id+"F8.opPattern","COPY",BODY,{"derivedFrom":makeQuery(id+"F7.opPattern","COPY",BODY,{"derivedFrom":makeQuery(id+"F6.opPattern","COPY",BODY,{"derivedFrom":makeQuery(id+"F5.opPattern","COPY",BODY,{"derivedFrom":makeQuery(id+"F4.opPattern","COPY",BODY,{"derivedFrom":makeQuery(id+"F3.opPattern","COPY",BODY,{"derivedFrom":makeQuery(id+"F2.opPattern","COPY",BODY,{"derivedFrom":makeQuery(id+"F1.opRevolve","SWEPT_BODY",BODY,{"disambiguationData":[OSD([sQuery(id+"F0.wireOp",EDGE,"E1")])]}),"instanceName":"1"}),"instanceName":"1"}),"instanceName":"1"}),"instanceName":"1"}),"instanceName":"1"}),"instanceName":"1"}),"instanceName":"1"});
            transform(context, id + "F9", {"entities" : qUnion([Q0, Q1, Q2, Q3, Q4, Q5, Q6, Q7, Q8, Q9, Q10, Q11, Q12, Q13, Q14, Q15, Q16, Q17, Q18, Q19, Q20, Q21, Q22, Q23, Q24, Q25, Q26, Q27, Q28, Q29, Q30, Q31, Q32, Q33, Q34, Q35, Q36, Q37, Q38, Q39, Q40, Q41, Q42, Q43, Q44, Q45, Q46, Q47, Q48, Q49, Q50, Q51, Q52, Q53, Q54, Q55, Q56, Q57, Q58, Q59, Q60, Q61, Q62, Q63, Q64, Q65, Q66, Q67, Q68, Q69, Q70, Q71, Q72, Q73, Q74, Q75, Q76, Q77, Q78, Q79, Q80, Q81, Q82, Q83, Q84, Q85, Q86, Q87, Q88, Q89, Q90, Q91, Q92, Q93, Q94, Q95]), "transformType" : TransformType.TRANSLATION_3D, "dx" : 13.44 * mm, "dy" : 0 * mm, "dz" : 0 * mm, "makeCopy" : true});
        }
        {
            var Q0;
            Q0=makeQuery(id+"F1.opRevolve","SWEPT_BODY",BODY,{"disambiguationData":[OSD([sQuery(id+"F0.wireOp",EDGE,"E1")])]});
            var Q1;
            Q1=makeQuery(id+"F3.opPattern","COPY",BODY,{"derivedFrom":makeQuery(id+"F2.opPattern","COPY",BODY,{"derivedFrom":makeQuery(id+"F1.opRevolve","SWEPT_BODY",BODY,{"disambiguationData":[OSD([sQuery(id+"F0.wireOp",EDGE,"E1")])]}),"instanceName":"1"}),"instanceName":"1"});
            var Q2;
            Q2=makeQuery(id+"F2.opPattern","COPY",BODY,{"derivedFrom":makeQuery(id+"F1.opRevolve","SWEPT_BODY",BODY,{"disambiguationData":[OSD([sQuery(id+"F0.wireOp",EDGE,"E1")])]}),"instanceName":"1"});
            var Q3;
            Q3=makeQuery(id+"F4.opPattern","COPY",BODY,{"derivedFrom":makeQuery(id+"F1.opRevolve","SWEPT_BODY",BODY,{"disambiguationData":[OSD([sQuery(id+"F0.wireOp",EDGE,"E1")])]}),"instanceName":"1"});
            var Q4;
            Q4=makeQuery(id+"F5.opPattern","COPY",BODY,{"derivedFrom":makeQuery(id+"F1.opRevolve","SWEPT_BODY",BODY,{"disambiguationData":[OSD([sQuery(id+"F0.wireOp",EDGE,"E1")])]}),"instanceName":"1"});
            var Q5;
            Q5=makeQuery(id+"F4.opPattern","COPY",BODY,{"derivedFrom":makeQuery(id+"F2.opPattern","COPY",BODY,{"derivedFrom":makeQuery(id+"F1.opRevolve","SWEPT_BODY",BODY,{"disambiguationData":[OSD([sQuery(id+"F0.wireOp",EDGE,"E1")])]}),"instanceName":"1"}),"instanceName":"1"});
            var Q6;
            Q6=makeQuery(id+"F4.opPattern","COPY",BODY,{"derivedFrom":makeQuery(id+"F3.opPattern","COPY",BODY,{"derivedFrom":makeQuery(id+"F2.opPattern","COPY",BODY,{"derivedFrom":makeQuery(id+"F1.opRevolve","SWEPT_BODY",BODY,{"disambiguationData":[OSD([sQuery(id+"F0.wireOp",EDGE,"E1")])]}),"instanceName":"1"}),"instanceName":"1"}),"instanceName":"1"});
            var Q7;
            Q7=makeQuery(id+"F7.opPattern","COPY",BODY,{"derivedFrom":makeQuery(id+"F4.opPattern","COPY",BODY,{"derivedFrom":makeQuery(id+"F3.opPattern","COPY",BODY,{"derivedFrom":makeQuery(id+"F2.opPattern","COPY",BODY,{"derivedFrom":makeQuery(id+"F1.opRevolve","SWEPT_BODY",BODY,{"disambiguationData":[OSD([sQuery(id+"F0.wireOp",EDGE,"E1")])]}),"instanceName":"1"}),"instanceName":"1"}),"instanceName":"1"}),"instanceName":"1"});
            var Q8;
            Q8=makeQuery(id+"F7.opPattern","COPY",BODY,{"derivedFrom":makeQuery(id+"F4.opPattern","COPY",BODY,{"derivedFrom":makeQuery(id+"F2.opPattern","COPY",BODY,{"derivedFrom":makeQuery(id+"F1.opRevolve","SWEPT_BODY",BODY,{"disambiguationData":[OSD([sQuery(id+"F0.wireOp",EDGE,"E1")])]}),"instanceName":"1"}),"instanceName":"1"}),"instanceName":"1"});
            var Q9;
            Q9=makeQuery(id+"F7.opPattern","COPY",BODY,{"derivedFrom":makeQuery(id+"F4.opPattern","COPY",BODY,{"derivedFrom":makeQuery(id+"F1.opRevolve","SWEPT_BODY",BODY,{"disambiguationData":[OSD([sQuery(id+"F0.wireOp",EDGE,"E1")])]}),"instanceName":"1"}),"instanceName":"1"});
            var Q10;
            Q10=makeQuery(id+"F7.opPattern","COPY",BODY,{"derivedFrom":makeQuery(id+"F3.opPattern","COPY",BODY,{"derivedFrom":makeQuery(id+"F2.opPattern","COPY",BODY,{"derivedFrom":makeQuery(id+"F1.opRevolve","SWEPT_BODY",BODY,{"disambiguationData":[OSD([sQuery(id+"F0.wireOp",EDGE,"E1")])]}),"instanceName":"1"}),"instanceName":"1"}),"instanceName":"1"});
            var Q11;
            Q11=makeQuery(id+"F7.opPattern","COPY",BODY,{"derivedFrom":makeQuery(id+"F2.opPattern","COPY",BODY,{"derivedFrom":makeQuery(id+"F1.opRevolve","SWEPT_BODY",BODY,{"disambiguationData":[OSD([sQuery(id+"F0.wireOp",EDGE,"E1")])]}),"instanceName":"1"}),"instanceName":"1"});
            var Q12;
            Q12=makeQuery(id+"F7.opPattern","COPY",BODY,{"derivedFrom":makeQuery(id+"F1.opRevolve","SWEPT_BODY",BODY,{"disambiguationData":[OSD([sQuery(id+"F0.wireOp",EDGE,"E1")])]}),"instanceName":"1"});
            var Q13;
            Q13=makeQuery(id+"F6.opPattern","COPY",BODY,{"derivedFrom":makeQuery(id+"F1.opRevolve","SWEPT_BODY",BODY,{"disambiguationData":[OSD([sQuery(id+"F0.wireOp",EDGE,"E1")])]}),"instanceName":"1"});
            var Q14;
            Q14=makeQuery(id+"F5.opPattern","COPY",BODY,{"derivedFrom":makeQuery(id+"F2.opPattern","COPY",BODY,{"derivedFrom":makeQuery(id+"F1.opRevolve","SWEPT_BODY",BODY,{"disambiguationData":[OSD([sQuery(id+"F0.wireOp",EDGE,"E1")])]}),"instanceName":"1"}),"instanceName":"1"});
            var Q15;
            Q15=makeQuery(id+"F5.opPattern","COPY",BODY,{"derivedFrom":makeQuery(id+"F3.opPattern","COPY",BODY,{"derivedFrom":makeQuery(id+"F2.opPattern","COPY",BODY,{"derivedFrom":makeQuery(id+"F1.opRevolve","SWEPT_BODY",BODY,{"disambiguationData":[OSD([sQuery(id+"F0.wireOp",EDGE,"E1")])]}),"instanceName":"1"}),"instanceName":"1"}),"instanceName":"1"});
            var Q16;
            Q16=makeQuery(id+"F5.opPattern","COPY",BODY,{"derivedFrom":makeQuery(id+"F4.opPattern","COPY",BODY,{"derivedFrom":makeQuery(id+"F1.opRevolve","SWEPT_BODY",BODY,{"disambiguationData":[OSD([sQuery(id+"F0.wireOp",EDGE,"E1")])]}),"instanceName":"1"}),"instanceName":"1"});
            var Q17;
            Q17=makeQuery(id+"F5.opPattern","COPY",BODY,{"derivedFrom":makeQuery(id+"F4.opPattern","COPY",BODY,{"derivedFrom":makeQuery(id+"F2.opPattern","COPY",BODY,{"derivedFrom":makeQuery(id+"F1.opRevolve","SWEPT_BODY",BODY,{"disambiguationData":[OSD([sQuery(id+"F0.wireOp",EDGE,"E1")])]}),"instanceName":"1"}),"instanceName":"1"}),"instanceName":"1"});
            var Q18;
            Q18=makeQuery(id+"F5.opPattern","COPY",BODY,{"derivedFrom":makeQuery(id+"F4.opPattern","COPY",BODY,{"derivedFrom":makeQuery(id+"F3.opPattern","COPY",BODY,{"derivedFrom":makeQuery(id+"F2.opPattern","COPY",BODY,{"derivedFrom":makeQuery(id+"F1.opRevolve","SWEPT_BODY",BODY,{"disambiguationData":[OSD([sQuery(id+"F0.wireOp",EDGE,"E1")])]}),"instanceName":"1"}),"instanceName":"1"}),"instanceName":"1"}),"instanceName":"1"});
            var Q19;
            Q19=makeQuery(id+"F7.opPattern","COPY",BODY,{"derivedFrom":makeQuery(id+"F5.opPattern","COPY",BODY,{"derivedFrom":makeQuery(id+"F1.opRevolve","SWEPT_BODY",BODY,{"disambiguationData":[OSD([sQuery(id+"F0.wireOp",EDGE,"E1")])]}),"instanceName":"1"}),"instanceName":"1"});
            var Q20;
            Q20=makeQuery(id+"F6.opPattern","COPY",BODY,{"derivedFrom":makeQuery(id+"F2.opPattern","COPY",BODY,{"derivedFrom":makeQuery(id+"F1.opRevolve","SWEPT_BODY",BODY,{"disambiguationData":[OSD([sQuery(id+"F0.wireOp",EDGE,"E1")])]}),"instanceName":"1"}),"instanceName":"1"});
            var Q21;
            Q21=makeQuery(id+"F6.opPattern","COPY",BODY,{"derivedFrom":makeQuery(id+"F3.opPattern","COPY",BODY,{"derivedFrom":makeQuery(id+"F2.opPattern","COPY",BODY,{"derivedFrom":makeQuery(id+"F1.opRevolve","SWEPT_BODY",BODY,{"disambiguationData":[OSD([sQuery(id+"F0.wireOp",EDGE,"E1")])]}),"instanceName":"1"}),"instanceName":"1"}),"instanceName":"1"});
            var Q22;
            Q22=makeQuery(id+"F6.opPattern","COPY",BODY,{"derivedFrom":makeQuery(id+"F4.opPattern","COPY",BODY,{"derivedFrom":makeQuery(id+"F1.opRevolve","SWEPT_BODY",BODY,{"disambiguationData":[OSD([sQuery(id+"F0.wireOp",EDGE,"E1")])]}),"instanceName":"1"}),"instanceName":"1"});
            var Q23;
            Q23=makeQuery(id+"F6.opPattern","COPY",BODY,{"derivedFrom":makeQuery(id+"F4.opPattern","COPY",BODY,{"derivedFrom":makeQuery(id+"F2.opPattern","COPY",BODY,{"derivedFrom":makeQuery(id+"F1.opRevolve","SWEPT_BODY",BODY,{"disambiguationData":[OSD([sQuery(id+"F0.wireOp",EDGE,"E1")])]}),"instanceName":"1"}),"instanceName":"1"}),"instanceName":"1"});
            var Q24;
            Q24=makeQuery(id+"F6.opPattern","COPY",BODY,{"derivedFrom":makeQuery(id+"F4.opPattern","COPY",BODY,{"derivedFrom":makeQuery(id+"F3.opPattern","COPY",BODY,{"derivedFrom":makeQuery(id+"F2.opPattern","COPY",BODY,{"derivedFrom":makeQuery(id+"F1.opRevolve","SWEPT_BODY",BODY,{"disambiguationData":[OSD([sQuery(id+"F0.wireOp",EDGE,"E1")])]}),"instanceName":"1"}),"instanceName":"1"}),"instanceName":"1"}),"instanceName":"1"});
            var Q25;
            Q25=makeQuery(id+"F6.opPattern","COPY",BODY,{"derivedFrom":makeQuery(id+"F5.opPattern","COPY",BODY,{"derivedFrom":makeQuery(id+"F1.opRevolve","SWEPT_BODY",BODY,{"disambiguationData":[OSD([sQuery(id+"F0.wireOp",EDGE,"E1")])]}),"instanceName":"1"}),"instanceName":"1"});
            var Q26;
            Q26=makeQuery(id+"F6.opPattern","COPY",BODY,{"derivedFrom":makeQuery(id+"F5.opPattern","COPY",BODY,{"derivedFrom":makeQuery(id+"F2.opPattern","COPY",BODY,{"derivedFrom":makeQuery(id+"F1.opRevolve","SWEPT_BODY",BODY,{"disambiguationData":[OSD([sQuery(id+"F0.wireOp",EDGE,"E1")])]}),"instanceName":"1"}),"instanceName":"1"}),"instanceName":"1"});
            var Q27;
            Q27=makeQuery(id+"F6.opPattern","COPY",BODY,{"derivedFrom":makeQuery(id+"F5.opPattern","COPY",BODY,{"derivedFrom":makeQuery(id+"F3.opPattern","COPY",BODY,{"derivedFrom":makeQuery(id+"F2.opPattern","COPY",BODY,{"derivedFrom":makeQuery(id+"F1.opRevolve","SWEPT_BODY",BODY,{"disambiguationData":[OSD([sQuery(id+"F0.wireOp",EDGE,"E1")])]}),"instanceName":"1"}),"instanceName":"1"}),"instanceName":"1"}),"instanceName":"1"});
            var Q28;
            Q28=makeQuery(id+"F6.opPattern","COPY",BODY,{"derivedFrom":makeQuery(id+"F5.opPattern","COPY",BODY,{"derivedFrom":makeQuery(id+"F4.opPattern","COPY",BODY,{"derivedFrom":makeQuery(id+"F1.opRevolve","SWEPT_BODY",BODY,{"disambiguationData":[OSD([sQuery(id+"F0.wireOp",EDGE,"E1")])]}),"instanceName":"1"}),"instanceName":"1"}),"instanceName":"1"});
            var Q29;
            Q29=makeQuery(id+"F6.opPattern","COPY",BODY,{"derivedFrom":makeQuery(id+"F5.opPattern","COPY",BODY,{"derivedFrom":makeQuery(id+"F4.opPattern","COPY",BODY,{"derivedFrom":makeQuery(id+"F2.opPattern","COPY",BODY,{"derivedFrom":makeQuery(id+"F1.opRevolve","SWEPT_BODY",BODY,{"disambiguationData":[OSD([sQuery(id+"F0.wireOp",EDGE,"E1")])]}),"instanceName":"1"}),"instanceName":"1"}),"instanceName":"1"}),"instanceName":"1"});
            var Q30;
            Q30=makeQuery(id+"F6.opPattern","COPY",BODY,{"derivedFrom":makeQuery(id+"F5.opPattern","COPY",BODY,{"derivedFrom":makeQuery(id+"F4.opPattern","COPY",BODY,{"derivedFrom":makeQuery(id+"F3.opPattern","COPY",BODY,{"derivedFrom":makeQuery(id+"F2.opPattern","COPY",BODY,{"derivedFrom":makeQuery(id+"F1.opRevolve","SWEPT_BODY",BODY,{"disambiguationData":[OSD([sQuery(id+"F0.wireOp",EDGE,"E1")])]}),"instanceName":"1"}),"instanceName":"1"}),"instanceName":"1"}),"instanceName":"1"}),"instanceName":"1"});
            var Q31;
            Q31=makeQuery(id+"F7.opPattern","COPY",BODY,{"derivedFrom":makeQuery(id+"F5.opPattern","COPY",BODY,{"derivedFrom":makeQuery(id+"F2.opPattern","COPY",BODY,{"derivedFrom":makeQuery(id+"F1.opRevolve","SWEPT_BODY",BODY,{"disambiguationData":[OSD([sQuery(id+"F0.wireOp",EDGE,"E1")])]}),"instanceName":"1"}),"instanceName":"1"}),"instanceName":"1"});
            var Q32;
            Q32=makeQuery(id+"F7.opPattern","COPY",BODY,{"derivedFrom":makeQuery(id+"F5.opPattern","COPY",BODY,{"derivedFrom":makeQuery(id+"F3.opPattern","COPY",BODY,{"derivedFrom":makeQuery(id+"F2.opPattern","COPY",BODY,{"derivedFrom":makeQuery(id+"F1.opRevolve","SWEPT_BODY",BODY,{"disambiguationData":[OSD([sQuery(id+"F0.wireOp",EDGE,"E1")])]}),"instanceName":"1"}),"instanceName":"1"}),"instanceName":"1"}),"instanceName":"1"});
            var Q33;
            Q33=makeQuery(id+"F7.opPattern","COPY",BODY,{"derivedFrom":makeQuery(id+"F5.opPattern","COPY",BODY,{"derivedFrom":makeQuery(id+"F4.opPattern","COPY",BODY,{"derivedFrom":makeQuery(id+"F1.opRevolve","SWEPT_BODY",BODY,{"disambiguationData":[OSD([sQuery(id+"F0.wireOp",EDGE,"E1")])]}),"instanceName":"1"}),"instanceName":"1"}),"instanceName":"1"});
            var Q34;
            Q34=makeQuery(id+"F7.opPattern","COPY",BODY,{"derivedFrom":makeQuery(id+"F5.opPattern","COPY",BODY,{"derivedFrom":makeQuery(id+"F4.opPattern","COPY",BODY,{"derivedFrom":makeQuery(id+"F2.opPattern","COPY",BODY,{"derivedFrom":makeQuery(id+"F1.opRevolve","SWEPT_BODY",BODY,{"disambiguationData":[OSD([sQuery(id+"F0.wireOp",EDGE,"E1")])]}),"instanceName":"1"}),"instanceName":"1"}),"instanceName":"1"}),"instanceName":"1"});
            var Q35;
            Q35=makeQuery(id+"F7.opPattern","COPY",BODY,{"derivedFrom":makeQuery(id+"F5.opPattern","COPY",BODY,{"derivedFrom":makeQuery(id+"F4.opPattern","COPY",BODY,{"derivedFrom":makeQuery(id+"F3.opPattern","COPY",BODY,{"derivedFrom":makeQuery(id+"F2.opPattern","COPY",BODY,{"derivedFrom":makeQuery(id+"F1.opRevolve","SWEPT_BODY",BODY,{"disambiguationData":[OSD([sQuery(id+"F0.wireOp",EDGE,"E1")])]}),"instanceName":"1"}),"instanceName":"1"}),"instanceName":"1"}),"instanceName":"1"}),"instanceName":"1"});
            var Q36;
            Q36=makeQuery(id+"F7.opPattern","COPY",BODY,{"derivedFrom":makeQuery(id+"F6.opPattern","COPY",BODY,{"derivedFrom":makeQuery(id+"F1.opRevolve","SWEPT_BODY",BODY,{"disambiguationData":[OSD([sQuery(id+"F0.wireOp",EDGE,"E1")])]}),"instanceName":"1"}),"instanceName":"1"});
            var Q37;
            Q37=makeQuery(id+"F7.opPattern","COPY",BODY,{"derivedFrom":makeQuery(id+"F6.opPattern","COPY",BODY,{"derivedFrom":makeQuery(id+"F2.opPattern","COPY",BODY,{"derivedFrom":makeQuery(id+"F1.opRevolve","SWEPT_BODY",BODY,{"disambiguationData":[OSD([sQuery(id+"F0.wireOp",EDGE,"E1")])]}),"instanceName":"1"}),"instanceName":"1"}),"instanceName":"1"});
            var Q38;
            Q38=makeQuery(id+"F7.opPattern","COPY",BODY,{"derivedFrom":makeQuery(id+"F6.opPattern","COPY",BODY,{"derivedFrom":makeQuery(id+"F3.opPattern","COPY",BODY,{"derivedFrom":makeQuery(id+"F2.opPattern","COPY",BODY,{"derivedFrom":makeQuery(id+"F1.opRevolve","SWEPT_BODY",BODY,{"disambiguationData":[OSD([sQuery(id+"F0.wireOp",EDGE,"E1")])]}),"instanceName":"1"}),"instanceName":"1"}),"instanceName":"1"}),"instanceName":"1"});
            var Q39;
            Q39=makeQuery(id+"F7.opPattern","COPY",BODY,{"derivedFrom":makeQuery(id+"F6.opPattern","COPY",BODY,{"derivedFrom":makeQuery(id+"F4.opPattern","COPY",BODY,{"derivedFrom":makeQuery(id+"F1.opRevolve","SWEPT_BODY",BODY,{"disambiguationData":[OSD([sQuery(id+"F0.wireOp",EDGE,"E1")])]}),"instanceName":"1"}),"instanceName":"1"}),"instanceName":"1"});
            var Q40;
            Q40=makeQuery(id+"F7.opPattern","COPY",BODY,{"derivedFrom":makeQuery(id+"F6.opPattern","COPY",BODY,{"derivedFrom":makeQuery(id+"F4.opPattern","COPY",BODY,{"derivedFrom":makeQuery(id+"F2.opPattern","COPY",BODY,{"derivedFrom":makeQuery(id+"F1.opRevolve","SWEPT_BODY",BODY,{"disambiguationData":[OSD([sQuery(id+"F0.wireOp",EDGE,"E1")])]}),"instanceName":"1"}),"instanceName":"1"}),"instanceName":"1"}),"instanceName":"1"});
            var Q41;
            Q41=makeQuery(id+"F7.opPattern","COPY",BODY,{"derivedFrom":makeQuery(id+"F6.opPattern","COPY",BODY,{"derivedFrom":makeQuery(id+"F4.opPattern","COPY",BODY,{"derivedFrom":makeQuery(id+"F3.opPattern","COPY",BODY,{"derivedFrom":makeQuery(id+"F2.opPattern","COPY",BODY,{"derivedFrom":makeQuery(id+"F1.opRevolve","SWEPT_BODY",BODY,{"disambiguationData":[OSD([sQuery(id+"F0.wireOp",EDGE,"E1")])]}),"instanceName":"1"}),"instanceName":"1"}),"instanceName":"1"}),"instanceName":"1"}),"instanceName":"1"});
            var Q42;
            Q42=makeQuery(id+"F7.opPattern","COPY",BODY,{"derivedFrom":makeQuery(id+"F6.opPattern","COPY",BODY,{"derivedFrom":makeQuery(id+"F5.opPattern","COPY",BODY,{"derivedFrom":makeQuery(id+"F1.opRevolve","SWEPT_BODY",BODY,{"disambiguationData":[OSD([sQuery(id+"F0.wireOp",EDGE,"E1")])]}),"instanceName":"1"}),"instanceName":"1"}),"instanceName":"1"});
            var Q43;
            Q43=makeQuery(id+"F7.opPattern","COPY",BODY,{"derivedFrom":makeQuery(id+"F6.opPattern","COPY",BODY,{"derivedFrom":makeQuery(id+"F5.opPattern","COPY",BODY,{"derivedFrom":makeQuery(id+"F2.opPattern","COPY",BODY,{"derivedFrom":makeQuery(id+"F1.opRevolve","SWEPT_BODY",BODY,{"disambiguationData":[OSD([sQuery(id+"F0.wireOp",EDGE,"E1")])]}),"instanceName":"1"}),"instanceName":"1"}),"instanceName":"1"}),"instanceName":"1"});
            var Q44;
            Q44=makeQuery(id+"F7.opPattern","COPY",BODY,{"derivedFrom":makeQuery(id+"F6.opPattern","COPY",BODY,{"derivedFrom":makeQuery(id+"F5.opPattern","COPY",BODY,{"derivedFrom":makeQuery(id+"F3.opPattern","COPY",BODY,{"derivedFrom":makeQuery(id+"F2.opPattern","COPY",BODY,{"derivedFrom":makeQuery(id+"F1.opRevolve","SWEPT_BODY",BODY,{"disambiguationData":[OSD([sQuery(id+"F0.wireOp",EDGE,"E1")])]}),"instanceName":"1"}),"instanceName":"1"}),"instanceName":"1"}),"instanceName":"1"}),"instanceName":"1"});
            var Q45;
            Q45=makeQuery(id+"F7.opPattern","COPY",BODY,{"derivedFrom":makeQuery(id+"F6.opPattern","COPY",BODY,{"derivedFrom":makeQuery(id+"F5.opPattern","COPY",BODY,{"derivedFrom":makeQuery(id+"F4.opPattern","COPY",BODY,{"derivedFrom":makeQuery(id+"F1.opRevolve","SWEPT_BODY",BODY,{"disambiguationData":[OSD([sQuery(id+"F0.wireOp",EDGE,"E1")])]}),"instanceName":"1"}),"instanceName":"1"}),"instanceName":"1"}),"instanceName":"1"});
            var Q46;
            Q46=makeQuery(id+"F7.opPattern","COPY",BODY,{"derivedFrom":makeQuery(id+"F6.opPattern","COPY",BODY,{"derivedFrom":makeQuery(id+"F5.opPattern","COPY",BODY,{"derivedFrom":makeQuery(id+"F4.opPattern","COPY",BODY,{"derivedFrom":makeQuery(id+"F2.opPattern","COPY",BODY,{"derivedFrom":makeQuery(id+"F1.opRevolve","SWEPT_BODY",BODY,{"disambiguationData":[OSD([sQuery(id+"F0.wireOp",EDGE,"E1")])]}),"instanceName":"1"}),"instanceName":"1"}),"instanceName":"1"}),"instanceName":"1"}),"instanceName":"1"});
            var Q47;
            Q47=makeQuery(id+"F7.opPattern","COPY",BODY,{"derivedFrom":makeQuery(id+"F6.opPattern","COPY",BODY,{"derivedFrom":makeQuery(id+"F5.opPattern","COPY",BODY,{"derivedFrom":makeQuery(id+"F4.opPattern","COPY",BODY,{"derivedFrom":makeQuery(id+"F3.opPattern","COPY",BODY,{"derivedFrom":makeQuery(id+"F2.opPattern","COPY",BODY,{"derivedFrom":makeQuery(id+"F1.opRevolve","SWEPT_BODY",BODY,{"disambiguationData":[OSD([sQuery(id+"F0.wireOp",EDGE,"E1")])]}),"instanceName":"1"}),"instanceName":"1"}),"instanceName":"1"}),"instanceName":"1"}),"instanceName":"1"}),"instanceName":"1"});
            var Q48;
            Q48=makeQuery(id+"F8.opPattern","COPY",BODY,{"derivedFrom":makeQuery(id+"F5.opPattern","COPY",BODY,{"derivedFrom":makeQuery(id+"F1.opRevolve","SWEPT_BODY",BODY,{"disambiguationData":[OSD([sQuery(id+"F0.wireOp",EDGE,"E1")])]}),"instanceName":"1"}),"instanceName":"1"});
            var Q49;
            Q49=makeQuery(id+"F8.opPattern","COPY",BODY,{"derivedFrom":makeQuery(id+"F4.opPattern","COPY",BODY,{"derivedFrom":makeQuery(id+"F3.opPattern","COPY",BODY,{"derivedFrom":makeQuery(id+"F2.opPattern","COPY",BODY,{"derivedFrom":makeQuery(id+"F1.opRevolve","SWEPT_BODY",BODY,{"disambiguationData":[OSD([sQuery(id+"F0.wireOp",EDGE,"E1")])]}),"instanceName":"1"}),"instanceName":"1"}),"instanceName":"1"}),"instanceName":"1"});
            var Q50;
            Q50=makeQuery(id+"F8.opPattern","COPY",BODY,{"derivedFrom":makeQuery(id+"F4.opPattern","COPY",BODY,{"derivedFrom":makeQuery(id+"F2.opPattern","COPY",BODY,{"derivedFrom":makeQuery(id+"F1.opRevolve","SWEPT_BODY",BODY,{"disambiguationData":[OSD([sQuery(id+"F0.wireOp",EDGE,"E1")])]}),"instanceName":"1"}),"instanceName":"1"}),"instanceName":"1"});
            var Q51;
            Q51=makeQuery(id+"F8.opPattern","COPY",BODY,{"derivedFrom":makeQuery(id+"F4.opPattern","COPY",BODY,{"derivedFrom":makeQuery(id+"F1.opRevolve","SWEPT_BODY",BODY,{"disambiguationData":[OSD([sQuery(id+"F0.wireOp",EDGE,"E1")])]}),"instanceName":"1"}),"instanceName":"1"});
            var Q52;
            Q52=makeQuery(id+"F8.opPattern","COPY",BODY,{"derivedFrom":makeQuery(id+"F3.opPattern","COPY",BODY,{"derivedFrom":makeQuery(id+"F2.opPattern","COPY",BODY,{"derivedFrom":makeQuery(id+"F1.opRevolve","SWEPT_BODY",BODY,{"disambiguationData":[OSD([sQuery(id+"F0.wireOp",EDGE,"E1")])]}),"instanceName":"1"}),"instanceName":"1"}),"instanceName":"1"});
            var Q53;
            Q53=makeQuery(id+"F8.opPattern","COPY",BODY,{"derivedFrom":makeQuery(id+"F2.opPattern","COPY",BODY,{"derivedFrom":makeQuery(id+"F1.opRevolve","SWEPT_BODY",BODY,{"disambiguationData":[OSD([sQuery(id+"F0.wireOp",EDGE,"E1")])]}),"instanceName":"1"}),"instanceName":"1"});
            var Q54;
            Q54=makeQuery(id+"F8.opPattern","COPY",BODY,{"derivedFrom":makeQuery(id+"F1.opRevolve","SWEPT_BODY",BODY,{"disambiguationData":[OSD([sQuery(id+"F0.wireOp",EDGE,"E1")])]}),"instanceName":"1"});
            var Q55;
            Q55=makeQuery(id+"F8.opPattern","COPY",BODY,{"derivedFrom":makeQuery(id+"F5.opPattern","COPY",BODY,{"derivedFrom":makeQuery(id+"F2.opPattern","COPY",BODY,{"derivedFrom":makeQuery(id+"F1.opRevolve","SWEPT_BODY",BODY,{"disambiguationData":[OSD([sQuery(id+"F0.wireOp",EDGE,"E1")])]}),"instanceName":"1"}),"instanceName":"1"}),"instanceName":"1"});
            var Q56;
            Q56=makeQuery(id+"F8.opPattern","COPY",BODY,{"derivedFrom":makeQuery(id+"F5.opPattern","COPY",BODY,{"derivedFrom":makeQuery(id+"F3.opPattern","COPY",BODY,{"derivedFrom":makeQuery(id+"F2.opPattern","COPY",BODY,{"derivedFrom":makeQuery(id+"F1.opRevolve","SWEPT_BODY",BODY,{"disambiguationData":[OSD([sQuery(id+"F0.wireOp",EDGE,"E1")])]}),"instanceName":"1"}),"instanceName":"1"}),"instanceName":"1"}),"instanceName":"1"});
            var Q57;
            Q57=makeQuery(id+"F8.opPattern","COPY",BODY,{"derivedFrom":makeQuery(id+"F5.opPattern","COPY",BODY,{"derivedFrom":makeQuery(id+"F4.opPattern","COPY",BODY,{"derivedFrom":makeQuery(id+"F1.opRevolve","SWEPT_BODY",BODY,{"disambiguationData":[OSD([sQuery(id+"F0.wireOp",EDGE,"E1")])]}),"instanceName":"1"}),"instanceName":"1"}),"instanceName":"1"});
            var Q58;
            Q58=makeQuery(id+"F8.opPattern","COPY",BODY,{"derivedFrom":makeQuery(id+"F5.opPattern","COPY",BODY,{"derivedFrom":makeQuery(id+"F4.opPattern","COPY",BODY,{"derivedFrom":makeQuery(id+"F2.opPattern","COPY",BODY,{"derivedFrom":makeQuery(id+"F1.opRevolve","SWEPT_BODY",BODY,{"disambiguationData":[OSD([sQuery(id+"F0.wireOp",EDGE,"E1")])]}),"instanceName":"1"}),"instanceName":"1"}),"instanceName":"1"}),"instanceName":"1"});
            var Q59;
            Q59=makeQuery(id+"F8.opPattern","COPY",BODY,{"derivedFrom":makeQuery(id+"F5.opPattern","COPY",BODY,{"derivedFrom":makeQuery(id+"F4.opPattern","COPY",BODY,{"derivedFrom":makeQuery(id+"F3.opPattern","COPY",BODY,{"derivedFrom":makeQuery(id+"F2.opPattern","COPY",BODY,{"derivedFrom":makeQuery(id+"F1.opRevolve","SWEPT_BODY",BODY,{"disambiguationData":[OSD([sQuery(id+"F0.wireOp",EDGE,"E1")])]}),"instanceName":"1"}),"instanceName":"1"}),"instanceName":"1"}),"instanceName":"1"}),"instanceName":"1"});
            var Q60;
            Q60=makeQuery(id+"F8.opPattern","COPY",BODY,{"derivedFrom":makeQuery(id+"F6.opPattern","COPY",BODY,{"derivedFrom":makeQuery(id+"F1.opRevolve","SWEPT_BODY",BODY,{"disambiguationData":[OSD([sQuery(id+"F0.wireOp",EDGE,"E1")])]}),"instanceName":"1"}),"instanceName":"1"});
            var Q61;
            Q61=makeQuery(id+"F8.opPattern","COPY",BODY,{"derivedFrom":makeQuery(id+"F6.opPattern","COPY",BODY,{"derivedFrom":makeQuery(id+"F2.opPattern","COPY",BODY,{"derivedFrom":makeQuery(id+"F1.opRevolve","SWEPT_BODY",BODY,{"disambiguationData":[OSD([sQuery(id+"F0.wireOp",EDGE,"E1")])]}),"instanceName":"1"}),"instanceName":"1"}),"instanceName":"1"});
            var Q62;
            Q62=makeQuery(id+"F8.opPattern","COPY",BODY,{"derivedFrom":makeQuery(id+"F6.opPattern","COPY",BODY,{"derivedFrom":makeQuery(id+"F3.opPattern","COPY",BODY,{"derivedFrom":makeQuery(id+"F2.opPattern","COPY",BODY,{"derivedFrom":makeQuery(id+"F1.opRevolve","SWEPT_BODY",BODY,{"disambiguationData":[OSD([sQuery(id+"F0.wireOp",EDGE,"E1")])]}),"instanceName":"1"}),"instanceName":"1"}),"instanceName":"1"}),"instanceName":"1"});
            var Q63;
            Q63=makeQuery(id+"F8.opPattern","COPY",BODY,{"derivedFrom":makeQuery(id+"F6.opPattern","COPY",BODY,{"derivedFrom":makeQuery(id+"F4.opPattern","COPY",BODY,{"derivedFrom":makeQuery(id+"F1.opRevolve","SWEPT_BODY",BODY,{"disambiguationData":[OSD([sQuery(id+"F0.wireOp",EDGE,"E1")])]}),"instanceName":"1"}),"instanceName":"1"}),"instanceName":"1"});
            var Q64;
            Q64=makeQuery(id+"F8.opPattern","COPY",BODY,{"derivedFrom":makeQuery(id+"F6.opPattern","COPY",BODY,{"derivedFrom":makeQuery(id+"F4.opPattern","COPY",BODY,{"derivedFrom":makeQuery(id+"F2.opPattern","COPY",BODY,{"derivedFrom":makeQuery(id+"F1.opRevolve","SWEPT_BODY",BODY,{"disambiguationData":[OSD([sQuery(id+"F0.wireOp",EDGE,"E1")])]}),"instanceName":"1"}),"instanceName":"1"}),"instanceName":"1"}),"instanceName":"1"});
            var Q65;
            Q65=makeQuery(id+"F8.opPattern","COPY",BODY,{"derivedFrom":makeQuery(id+"F6.opPattern","COPY",BODY,{"derivedFrom":makeQuery(id+"F4.opPattern","COPY",BODY,{"derivedFrom":makeQuery(id+"F3.opPattern","COPY",BODY,{"derivedFrom":makeQuery(id+"F2.opPattern","COPY",BODY,{"derivedFrom":makeQuery(id+"F1.opRevolve","SWEPT_BODY",BODY,{"disambiguationData":[OSD([sQuery(id+"F0.wireOp",EDGE,"E1")])]}),"instanceName":"1"}),"instanceName":"1"}),"instanceName":"1"}),"instanceName":"1"}),"instanceName":"1"});
            var Q66;
            Q66=makeQuery(id+"F8.opPattern","COPY",BODY,{"derivedFrom":makeQuery(id+"F6.opPattern","COPY",BODY,{"derivedFrom":makeQuery(id+"F5.opPattern","COPY",BODY,{"derivedFrom":makeQuery(id+"F1.opRevolve","SWEPT_BODY",BODY,{"disambiguationData":[OSD([sQuery(id+"F0.wireOp",EDGE,"E1")])]}),"instanceName":"1"}),"instanceName":"1"}),"instanceName":"1"});
            var Q67;
            Q67=makeQuery(id+"F8.opPattern","COPY",BODY,{"derivedFrom":makeQuery(id+"F6.opPattern","COPY",BODY,{"derivedFrom":makeQuery(id+"F5.opPattern","COPY",BODY,{"derivedFrom":makeQuery(id+"F2.opPattern","COPY",BODY,{"derivedFrom":makeQuery(id+"F1.opRevolve","SWEPT_BODY",BODY,{"disambiguationData":[OSD([sQuery(id+"F0.wireOp",EDGE,"E1")])]}),"instanceName":"1"}),"instanceName":"1"}),"instanceName":"1"}),"instanceName":"1"});
            var Q68;
            Q68=makeQuery(id+"F8.opPattern","COPY",BODY,{"derivedFrom":makeQuery(id+"F6.opPattern","COPY",BODY,{"derivedFrom":makeQuery(id+"F5.opPattern","COPY",BODY,{"derivedFrom":makeQuery(id+"F3.opPattern","COPY",BODY,{"derivedFrom":makeQuery(id+"F2.opPattern","COPY",BODY,{"derivedFrom":makeQuery(id+"F1.opRevolve","SWEPT_BODY",BODY,{"disambiguationData":[OSD([sQuery(id+"F0.wireOp",EDGE,"E1")])]}),"instanceName":"1"}),"instanceName":"1"}),"instanceName":"1"}),"instanceName":"1"}),"instanceName":"1"});
            var Q69;
            Q69=makeQuery(id+"F8.opPattern","COPY",BODY,{"derivedFrom":makeQuery(id+"F6.opPattern","COPY",BODY,{"derivedFrom":makeQuery(id+"F5.opPattern","COPY",BODY,{"derivedFrom":makeQuery(id+"F4.opPattern","COPY",BODY,{"derivedFrom":makeQuery(id+"F1.opRevolve","SWEPT_BODY",BODY,{"disambiguationData":[OSD([sQuery(id+"F0.wireOp",EDGE,"E1")])]}),"instanceName":"1"}),"instanceName":"1"}),"instanceName":"1"}),"instanceName":"1"});
            var Q70;
            Q70=makeQuery(id+"F8.opPattern","COPY",BODY,{"derivedFrom":makeQuery(id+"F6.opPattern","COPY",BODY,{"derivedFrom":makeQuery(id+"F5.opPattern","COPY",BODY,{"derivedFrom":makeQuery(id+"F4.opPattern","COPY",BODY,{"derivedFrom":makeQuery(id+"F2.opPattern","COPY",BODY,{"derivedFrom":makeQuery(id+"F1.opRevolve","SWEPT_BODY",BODY,{"disambiguationData":[OSD([sQuery(id+"F0.wireOp",EDGE,"E1")])]}),"instanceName":"1"}),"instanceName":"1"}),"instanceName":"1"}),"instanceName":"1"}),"instanceName":"1"});
            var Q71;
            Q71=makeQuery(id+"F8.opPattern","COPY",BODY,{"derivedFrom":makeQuery(id+"F6.opPattern","COPY",BODY,{"derivedFrom":makeQuery(id+"F5.opPattern","COPY",BODY,{"derivedFrom":makeQuery(id+"F4.opPattern","COPY",BODY,{"derivedFrom":makeQuery(id+"F3.opPattern","COPY",BODY,{"derivedFrom":makeQuery(id+"F2.opPattern","COPY",BODY,{"derivedFrom":makeQuery(id+"F1.opRevolve","SWEPT_BODY",BODY,{"disambiguationData":[OSD([sQuery(id+"F0.wireOp",EDGE,"E1")])]}),"instanceName":"1"}),"instanceName":"1"}),"instanceName":"1"}),"instanceName":"1"}),"instanceName":"1"}),"instanceName":"1"});
            var Q72;
            Q72=makeQuery(id+"F8.opPattern","COPY",BODY,{"derivedFrom":makeQuery(id+"F7.opPattern","COPY",BODY,{"derivedFrom":makeQuery(id+"F1.opRevolve","SWEPT_BODY",BODY,{"disambiguationData":[OSD([sQuery(id+"F0.wireOp",EDGE,"E1")])]}),"instanceName":"1"}),"instanceName":"1"});
            var Q73;
            Q73=makeQuery(id+"F8.opPattern","COPY",BODY,{"derivedFrom":makeQuery(id+"F7.opPattern","COPY",BODY,{"derivedFrom":makeQuery(id+"F2.opPattern","COPY",BODY,{"derivedFrom":makeQuery(id+"F1.opRevolve","SWEPT_BODY",BODY,{"disambiguationData":[OSD([sQuery(id+"F0.wireOp",EDGE,"E1")])]}),"instanceName":"1"}),"instanceName":"1"}),"instanceName":"1"});
            var Q74;
            Q74=makeQuery(id+"F8.opPattern","COPY",BODY,{"derivedFrom":makeQuery(id+"F7.opPattern","COPY",BODY,{"derivedFrom":makeQuery(id+"F3.opPattern","COPY",BODY,{"derivedFrom":makeQuery(id+"F2.opPattern","COPY",BODY,{"derivedFrom":makeQuery(id+"F1.opRevolve","SWEPT_BODY",BODY,{"disambiguationData":[OSD([sQuery(id+"F0.wireOp",EDGE,"E1")])]}),"instanceName":"1"}),"instanceName":"1"}),"instanceName":"1"}),"instanceName":"1"});
            var Q75;
            Q75=makeQuery(id+"F8.opPattern","COPY",BODY,{"derivedFrom":makeQuery(id+"F7.opPattern","COPY",BODY,{"derivedFrom":makeQuery(id+"F4.opPattern","COPY",BODY,{"derivedFrom":makeQuery(id+"F1.opRevolve","SWEPT_BODY",BODY,{"disambiguationData":[OSD([sQuery(id+"F0.wireOp",EDGE,"E1")])]}),"instanceName":"1"}),"instanceName":"1"}),"instanceName":"1"});
            var Q76;
            Q76=makeQuery(id+"F8.opPattern","COPY",BODY,{"derivedFrom":makeQuery(id+"F7.opPattern","COPY",BODY,{"derivedFrom":makeQuery(id+"F4.opPattern","COPY",BODY,{"derivedFrom":makeQuery(id+"F2.opPattern","COPY",BODY,{"derivedFrom":makeQuery(id+"F1.opRevolve","SWEPT_BODY",BODY,{"disambiguationData":[OSD([sQuery(id+"F0.wireOp",EDGE,"E1")])]}),"instanceName":"1"}),"instanceName":"1"}),"instanceName":"1"}),"instanceName":"1"});
            var Q77;
            Q77=makeQuery(id+"F8.opPattern","COPY",BODY,{"derivedFrom":makeQuery(id+"F7.opPattern","COPY",BODY,{"derivedFrom":makeQuery(id+"F4.opPattern","COPY",BODY,{"derivedFrom":makeQuery(id+"F3.opPattern","COPY",BODY,{"derivedFrom":makeQuery(id+"F2.opPattern","COPY",BODY,{"derivedFrom":makeQuery(id+"F1.opRevolve","SWEPT_BODY",BODY,{"disambiguationData":[OSD([sQuery(id+"F0.wireOp",EDGE,"E1")])]}),"instanceName":"1"}),"instanceName":"1"}),"instanceName":"1"}),"instanceName":"1"}),"instanceName":"1"});
            var Q78;
            Q78=makeQuery(id+"F8.opPattern","COPY",BODY,{"derivedFrom":makeQuery(id+"F7.opPattern","COPY",BODY,{"derivedFrom":makeQuery(id+"F5.opPattern","COPY",BODY,{"derivedFrom":makeQuery(id+"F1.opRevolve","SWEPT_BODY",BODY,{"disambiguationData":[OSD([sQuery(id+"F0.wireOp",EDGE,"E1")])]}),"instanceName":"1"}),"instanceName":"1"}),"instanceName":"1"});
            var Q79;
            Q79=makeQuery(id+"F8.opPattern","COPY",BODY,{"derivedFrom":makeQuery(id+"F7.opPattern","COPY",BODY,{"derivedFrom":makeQuery(id+"F5.opPattern","COPY",BODY,{"derivedFrom":makeQuery(id+"F2.opPattern","COPY",BODY,{"derivedFrom":makeQuery(id+"F1.opRevolve","SWEPT_BODY",BODY,{"disambiguationData":[OSD([sQuery(id+"F0.wireOp",EDGE,"E1")])]}),"instanceName":"1"}),"instanceName":"1"}),"instanceName":"1"}),"instanceName":"1"});
            var Q80;
            Q80=makeQuery(id+"F8.opPattern","COPY",BODY,{"derivedFrom":makeQuery(id+"F7.opPattern","COPY",BODY,{"derivedFrom":makeQuery(id+"F5.opPattern","COPY",BODY,{"derivedFrom":makeQuery(id+"F3.opPattern","COPY",BODY,{"derivedFrom":makeQuery(id+"F2.opPattern","COPY",BODY,{"derivedFrom":makeQuery(id+"F1.opRevolve","SWEPT_BODY",BODY,{"disambiguationData":[OSD([sQuery(id+"F0.wireOp",EDGE,"E1")])]}),"instanceName":"1"}),"instanceName":"1"}),"instanceName":"1"}),"instanceName":"1"}),"instanceName":"1"});
            var Q81;
            Q81=makeQuery(id+"F8.opPattern","COPY",BODY,{"derivedFrom":makeQuery(id+"F7.opPattern","COPY",BODY,{"derivedFrom":makeQuery(id+"F5.opPattern","COPY",BODY,{"derivedFrom":makeQuery(id+"F4.opPattern","COPY",BODY,{"derivedFrom":makeQuery(id+"F1.opRevolve","SWEPT_BODY",BODY,{"disambiguationData":[OSD([sQuery(id+"F0.wireOp",EDGE,"E1")])]}),"instanceName":"1"}),"instanceName":"1"}),"instanceName":"1"}),"instanceName":"1"});
            var Q82;
            Q82=makeQuery(id+"F8.opPattern","COPY",BODY,{"derivedFrom":makeQuery(id+"F7.opPattern","COPY",BODY,{"derivedFrom":makeQuery(id+"F5.opPattern","COPY",BODY,{"derivedFrom":makeQuery(id+"F4.opPattern","COPY",BODY,{"derivedFrom":makeQuery(id+"F2.opPattern","COPY",BODY,{"derivedFrom":makeQuery(id+"F1.opRevolve","SWEPT_BODY",BODY,{"disambiguationData":[OSD([sQuery(id+"F0.wireOp",EDGE,"E1")])]}),"instanceName":"1"}),"instanceName":"1"}),"instanceName":"1"}),"instanceName":"1"}),"instanceName":"1"});
            var Q83;
            Q83=makeQuery(id+"F8.opPattern","COPY",BODY,{"derivedFrom":makeQuery(id+"F7.opPattern","COPY",BODY,{"derivedFrom":makeQuery(id+"F5.opPattern","COPY",BODY,{"derivedFrom":makeQuery(id+"F4.opPattern","COPY",BODY,{"derivedFrom":makeQuery(id+"F3.opPattern","COPY",BODY,{"derivedFrom":makeQuery(id+"F2.opPattern","COPY",BODY,{"derivedFrom":makeQuery(id+"F1.opRevolve","SWEPT_BODY",BODY,{"disambiguationData":[OSD([sQuery(id+"F0.wireOp",EDGE,"E1")])]}),"instanceName":"1"}),"instanceName":"1"}),"instanceName":"1"}),"instanceName":"1"}),"instanceName":"1"}),"instanceName":"1"});
            var Q84;
            Q84=makeQuery(id+"F8.opPattern","COPY",BODY,{"derivedFrom":makeQuery(id+"F7.opPattern","COPY",BODY,{"derivedFrom":makeQuery(id+"F6.opPattern","COPY",BODY,{"derivedFrom":makeQuery(id+"F1.opRevolve","SWEPT_BODY",BODY,{"disambiguationData":[OSD([sQuery(id+"F0.wireOp",EDGE,"E1")])]}),"instanceName":"1"}),"instanceName":"1"}),"instanceName":"1"});
            var Q85;
            Q85=makeQuery(id+"F8.opPattern","COPY",BODY,{"derivedFrom":makeQuery(id+"F7.opPattern","COPY",BODY,{"derivedFrom":makeQuery(id+"F6.opPattern","COPY",BODY,{"derivedFrom":makeQuery(id+"F2.opPattern","COPY",BODY,{"derivedFrom":makeQuery(id+"F1.opRevolve","SWEPT_BODY",BODY,{"disambiguationData":[OSD([sQuery(id+"F0.wireOp",EDGE,"E1")])]}),"instanceName":"1"}),"instanceName":"1"}),"instanceName":"1"}),"instanceName":"1"});
            var Q86;
            Q86=makeQuery(id+"F8.opPattern","COPY",BODY,{"derivedFrom":makeQuery(id+"F7.opPattern","COPY",BODY,{"derivedFrom":makeQuery(id+"F6.opPattern","COPY",BODY,{"derivedFrom":makeQuery(id+"F3.opPattern","COPY",BODY,{"derivedFrom":makeQuery(id+"F2.opPattern","COPY",BODY,{"derivedFrom":makeQuery(id+"F1.opRevolve","SWEPT_BODY",BODY,{"disambiguationData":[OSD([sQuery(id+"F0.wireOp",EDGE,"E1")])]}),"instanceName":"1"}),"instanceName":"1"}),"instanceName":"1"}),"instanceName":"1"}),"instanceName":"1"});
            var Q87;
            Q87=makeQuery(id+"F8.opPattern","COPY",BODY,{"derivedFrom":makeQuery(id+"F7.opPattern","COPY",BODY,{"derivedFrom":makeQuery(id+"F6.opPattern","COPY",BODY,{"derivedFrom":makeQuery(id+"F4.opPattern","COPY",BODY,{"derivedFrom":makeQuery(id+"F1.opRevolve","SWEPT_BODY",BODY,{"disambiguationData":[OSD([sQuery(id+"F0.wireOp",EDGE,"E1")])]}),"instanceName":"1"}),"instanceName":"1"}),"instanceName":"1"}),"instanceName":"1"});
            var Q88;
            Q88=makeQuery(id+"F8.opPattern","COPY",BODY,{"derivedFrom":makeQuery(id+"F7.opPattern","COPY",BODY,{"derivedFrom":makeQuery(id+"F6.opPattern","COPY",BODY,{"derivedFrom":makeQuery(id+"F4.opPattern","COPY",BODY,{"derivedFrom":makeQuery(id+"F2.opPattern","COPY",BODY,{"derivedFrom":makeQuery(id+"F1.opRevolve","SWEPT_BODY",BODY,{"disambiguationData":[OSD([sQuery(id+"F0.wireOp",EDGE,"E1")])]}),"instanceName":"1"}),"instanceName":"1"}),"instanceName":"1"}),"instanceName":"1"}),"instanceName":"1"});
            var Q89;
            Q89=makeQuery(id+"F8.opPattern","COPY",BODY,{"derivedFrom":makeQuery(id+"F7.opPattern","COPY",BODY,{"derivedFrom":makeQuery(id+"F6.opPattern","COPY",BODY,{"derivedFrom":makeQuery(id+"F4.opPattern","COPY",BODY,{"derivedFrom":makeQuery(id+"F3.opPattern","COPY",BODY,{"derivedFrom":makeQuery(id+"F2.opPattern","COPY",BODY,{"derivedFrom":makeQuery(id+"F1.opRevolve","SWEPT_BODY",BODY,{"disambiguationData":[OSD([sQuery(id+"F0.wireOp",EDGE,"E1")])]}),"instanceName":"1"}),"instanceName":"1"}),"instanceName":"1"}),"instanceName":"1"}),"instanceName":"1"}),"instanceName":"1"});
            var Q90;
            Q90=makeQuery(id+"F8.opPattern","COPY",BODY,{"derivedFrom":makeQuery(id+"F7.opPattern","COPY",BODY,{"derivedFrom":makeQuery(id+"F6.opPattern","COPY",BODY,{"derivedFrom":makeQuery(id+"F5.opPattern","COPY",BODY,{"derivedFrom":makeQuery(id+"F1.opRevolve","SWEPT_BODY",BODY,{"disambiguationData":[OSD([sQuery(id+"F0.wireOp",EDGE,"E1")])]}),"instanceName":"1"}),"instanceName":"1"}),"instanceName":"1"}),"instanceName":"1"});
            var Q91;
            Q91=makeQuery(id+"F8.opPattern","COPY",BODY,{"derivedFrom":makeQuery(id+"F7.opPattern","COPY",BODY,{"derivedFrom":makeQuery(id+"F6.opPattern","COPY",BODY,{"derivedFrom":makeQuery(id+"F5.opPattern","COPY",BODY,{"derivedFrom":makeQuery(id+"F2.opPattern","COPY",BODY,{"derivedFrom":makeQuery(id+"F1.opRevolve","SWEPT_BODY",BODY,{"disambiguationData":[OSD([sQuery(id+"F0.wireOp",EDGE,"E1")])]}),"instanceName":"1"}),"instanceName":"1"}),"instanceName":"1"}),"instanceName":"1"}),"instanceName":"1"});
            var Q92;
            Q92=makeQuery(id+"F8.opPattern","COPY",BODY,{"derivedFrom":makeQuery(id+"F7.opPattern","COPY",BODY,{"derivedFrom":makeQuery(id+"F6.opPattern","COPY",BODY,{"derivedFrom":makeQuery(id+"F5.opPattern","COPY",BODY,{"derivedFrom":makeQuery(id+"F3.opPattern","COPY",BODY,{"derivedFrom":makeQuery(id+"F2.opPattern","COPY",BODY,{"derivedFrom":makeQuery(id+"F1.opRevolve","SWEPT_BODY",BODY,{"disambiguationData":[OSD([sQuery(id+"F0.wireOp",EDGE,"E1")])]}),"instanceName":"1"}),"instanceName":"1"}),"instanceName":"1"}),"instanceName":"1"}),"instanceName":"1"}),"instanceName":"1"});
            var Q93;
            Q93=makeQuery(id+"F8.opPattern","COPY",BODY,{"derivedFrom":makeQuery(id+"F7.opPattern","COPY",BODY,{"derivedFrom":makeQuery(id+"F6.opPattern","COPY",BODY,{"derivedFrom":makeQuery(id+"F5.opPattern","COPY",BODY,{"derivedFrom":makeQuery(id+"F4.opPattern","COPY",BODY,{"derivedFrom":makeQuery(id+"F1.opRevolve","SWEPT_BODY",BODY,{"disambiguationData":[OSD([sQuery(id+"F0.wireOp",EDGE,"E1")])]}),"instanceName":"1"}),"instanceName":"1"}),"instanceName":"1"}),"instanceName":"1"}),"instanceName":"1"});
            var Q94;
            Q94=makeQuery(id+"F8.opPattern","COPY",BODY,{"derivedFrom":makeQuery(id+"F7.opPattern","COPY",BODY,{"derivedFrom":makeQuery(id+"F6.opPattern","COPY",BODY,{"derivedFrom":makeQuery(id+"F5.opPattern","COPY",BODY,{"derivedFrom":makeQuery(id+"F4.opPattern","COPY",BODY,{"derivedFrom":makeQuery(id+"F2.opPattern","COPY",BODY,{"derivedFrom":makeQuery(id+"F1.opRevolve","SWEPT_BODY",BODY,{"disambiguationData":[OSD([sQuery(id+"F0.wireOp",EDGE,"E1")])]}),"instanceName":"1"}),"instanceName":"1"}),"instanceName":"1"}),"instanceName":"1"}),"instanceName":"1"}),"instanceName":"1"});
            var Q95;
            Q95=makeQuery(id+"F8.opPattern","COPY",BODY,{"derivedFrom":makeQuery(id+"F7.opPattern","COPY",BODY,{"derivedFrom":makeQuery(id+"F6.opPattern","COPY",BODY,{"derivedFrom":makeQuery(id+"F5.opPattern","COPY",BODY,{"derivedFrom":makeQuery(id+"F4.opPattern","COPY",BODY,{"derivedFrom":makeQuery(id+"F3.opPattern","COPY",BODY,{"derivedFrom":makeQuery(id+"F2.opPattern","COPY",BODY,{"derivedFrom":makeQuery(id+"F1.opRevolve","SWEPT_BODY",BODY,{"disambiguationData":[OSD([sQuery(id+"F0.wireOp",EDGE,"E1")])]}),"instanceName":"1"}),"instanceName":"1"}),"instanceName":"1"}),"instanceName":"1"}),"instanceName":"1"}),"instanceName":"1"}),"instanceName":"1"});
            var Q96;
            Q96=makeQuery(id+"F9.opPattern","COPY",BODY,{"derivedFrom":makeQuery(id+"F5.opPattern","COPY",BODY,{"derivedFrom":makeQuery(id+"F1.opRevolve","SWEPT_BODY",BODY,{"disambiguationData":[OSD([sQuery(id+"F0.wireOp",EDGE,"E1")])]}),"instanceName":"1"}),"instanceName":"1"});
            var Q97;
            Q97=makeQuery(id+"F9.opPattern","COPY",BODY,{"derivedFrom":makeQuery(id+"F4.opPattern","COPY",BODY,{"derivedFrom":makeQuery(id+"F3.opPattern","COPY",BODY,{"derivedFrom":makeQuery(id+"F2.opPattern","COPY",BODY,{"derivedFrom":makeQuery(id+"F1.opRevolve","SWEPT_BODY",BODY,{"disambiguationData":[OSD([sQuery(id+"F0.wireOp",EDGE,"E1")])]}),"instanceName":"1"}),"instanceName":"1"}),"instanceName":"1"}),"instanceName":"1"});
            var Q98;
            Q98=makeQuery(id+"F9.opPattern","COPY",BODY,{"derivedFrom":makeQuery(id+"F4.opPattern","COPY",BODY,{"derivedFrom":makeQuery(id+"F2.opPattern","COPY",BODY,{"derivedFrom":makeQuery(id+"F1.opRevolve","SWEPT_BODY",BODY,{"disambiguationData":[OSD([sQuery(id+"F0.wireOp",EDGE,"E1")])]}),"instanceName":"1"}),"instanceName":"1"}),"instanceName":"1"});
            var Q99;
            Q99=makeQuery(id+"F9.opPattern","COPY",BODY,{"derivedFrom":makeQuery(id+"F4.opPattern","COPY",BODY,{"derivedFrom":makeQuery(id+"F1.opRevolve","SWEPT_BODY",BODY,{"disambiguationData":[OSD([sQuery(id+"F0.wireOp",EDGE,"E1")])]}),"instanceName":"1"}),"instanceName":"1"});
            var Q100;
            Q100=makeQuery(id+"F9.opPattern","COPY",BODY,{"derivedFrom":makeQuery(id+"F3.opPattern","COPY",BODY,{"derivedFrom":makeQuery(id+"F2.opPattern","COPY",BODY,{"derivedFrom":makeQuery(id+"F1.opRevolve","SWEPT_BODY",BODY,{"disambiguationData":[OSD([sQuery(id+"F0.wireOp",EDGE,"E1")])]}),"instanceName":"1"}),"instanceName":"1"}),"instanceName":"1"});
            var Q101;
            Q101=makeQuery(id+"F9.opPattern","COPY",BODY,{"derivedFrom":makeQuery(id+"F2.opPattern","COPY",BODY,{"derivedFrom":makeQuery(id+"F1.opRevolve","SWEPT_BODY",BODY,{"disambiguationData":[OSD([sQuery(id+"F0.wireOp",EDGE,"E1")])]}),"instanceName":"1"}),"instanceName":"1"});
            var Q102;
            Q102=makeQuery(id+"F9.opPattern","COPY",BODY,{"derivedFrom":makeQuery(id+"F1.opRevolve","SWEPT_BODY",BODY,{"disambiguationData":[OSD([sQuery(id+"F0.wireOp",EDGE,"E1")])]}),"instanceName":"1"});
            var Q103;
            Q103=makeQuery(id+"F9.opPattern","COPY",BODY,{"derivedFrom":makeQuery(id+"F5.opPattern","COPY",BODY,{"derivedFrom":makeQuery(id+"F2.opPattern","COPY",BODY,{"derivedFrom":makeQuery(id+"F1.opRevolve","SWEPT_BODY",BODY,{"disambiguationData":[OSD([sQuery(id+"F0.wireOp",EDGE,"E1")])]}),"instanceName":"1"}),"instanceName":"1"}),"instanceName":"1"});
            var Q104;
            Q104=makeQuery(id+"F9.opPattern","COPY",BODY,{"derivedFrom":makeQuery(id+"F5.opPattern","COPY",BODY,{"derivedFrom":makeQuery(id+"F3.opPattern","COPY",BODY,{"derivedFrom":makeQuery(id+"F2.opPattern","COPY",BODY,{"derivedFrom":makeQuery(id+"F1.opRevolve","SWEPT_BODY",BODY,{"disambiguationData":[OSD([sQuery(id+"F0.wireOp",EDGE,"E1")])]}),"instanceName":"1"}),"instanceName":"1"}),"instanceName":"1"}),"instanceName":"1"});
            var Q105;
            Q105=makeQuery(id+"F9.opPattern","COPY",BODY,{"derivedFrom":makeQuery(id+"F5.opPattern","COPY",BODY,{"derivedFrom":makeQuery(id+"F4.opPattern","COPY",BODY,{"derivedFrom":makeQuery(id+"F1.opRevolve","SWEPT_BODY",BODY,{"disambiguationData":[OSD([sQuery(id+"F0.wireOp",EDGE,"E1")])]}),"instanceName":"1"}),"instanceName":"1"}),"instanceName":"1"});
            var Q106;
            Q106=makeQuery(id+"F9.opPattern","COPY",BODY,{"derivedFrom":makeQuery(id+"F5.opPattern","COPY",BODY,{"derivedFrom":makeQuery(id+"F4.opPattern","COPY",BODY,{"derivedFrom":makeQuery(id+"F2.opPattern","COPY",BODY,{"derivedFrom":makeQuery(id+"F1.opRevolve","SWEPT_BODY",BODY,{"disambiguationData":[OSD([sQuery(id+"F0.wireOp",EDGE,"E1")])]}),"instanceName":"1"}),"instanceName":"1"}),"instanceName":"1"}),"instanceName":"1"});
            var Q107;
            Q107=makeQuery(id+"F9.opPattern","COPY",BODY,{"derivedFrom":makeQuery(id+"F5.opPattern","COPY",BODY,{"derivedFrom":makeQuery(id+"F4.opPattern","COPY",BODY,{"derivedFrom":makeQuery(id+"F3.opPattern","COPY",BODY,{"derivedFrom":makeQuery(id+"F2.opPattern","COPY",BODY,{"derivedFrom":makeQuery(id+"F1.opRevolve","SWEPT_BODY",BODY,{"disambiguationData":[OSD([sQuery(id+"F0.wireOp",EDGE,"E1")])]}),"instanceName":"1"}),"instanceName":"1"}),"instanceName":"1"}),"instanceName":"1"}),"instanceName":"1"});
            var Q108;
            Q108=makeQuery(id+"F9.opPattern","COPY",BODY,{"derivedFrom":makeQuery(id+"F6.opPattern","COPY",BODY,{"derivedFrom":makeQuery(id+"F1.opRevolve","SWEPT_BODY",BODY,{"disambiguationData":[OSD([sQuery(id+"F0.wireOp",EDGE,"E1")])]}),"instanceName":"1"}),"instanceName":"1"});
            var Q109;
            Q109=makeQuery(id+"F9.opPattern","COPY",BODY,{"derivedFrom":makeQuery(id+"F6.opPattern","COPY",BODY,{"derivedFrom":makeQuery(id+"F2.opPattern","COPY",BODY,{"derivedFrom":makeQuery(id+"F1.opRevolve","SWEPT_BODY",BODY,{"disambiguationData":[OSD([sQuery(id+"F0.wireOp",EDGE,"E1")])]}),"instanceName":"1"}),"instanceName":"1"}),"instanceName":"1"});
            var Q110;
            Q110=makeQuery(id+"F9.opPattern","COPY",BODY,{"derivedFrom":makeQuery(id+"F6.opPattern","COPY",BODY,{"derivedFrom":makeQuery(id+"F3.opPattern","COPY",BODY,{"derivedFrom":makeQuery(id+"F2.opPattern","COPY",BODY,{"derivedFrom":makeQuery(id+"F1.opRevolve","SWEPT_BODY",BODY,{"disambiguationData":[OSD([sQuery(id+"F0.wireOp",EDGE,"E1")])]}),"instanceName":"1"}),"instanceName":"1"}),"instanceName":"1"}),"instanceName":"1"});
            var Q111;
            Q111=makeQuery(id+"F9.opPattern","COPY",BODY,{"derivedFrom":makeQuery(id+"F6.opPattern","COPY",BODY,{"derivedFrom":makeQuery(id+"F4.opPattern","COPY",BODY,{"derivedFrom":makeQuery(id+"F1.opRevolve","SWEPT_BODY",BODY,{"disambiguationData":[OSD([sQuery(id+"F0.wireOp",EDGE,"E1")])]}),"instanceName":"1"}),"instanceName":"1"}),"instanceName":"1"});
            var Q112;
            Q112=makeQuery(id+"F9.opPattern","COPY",BODY,{"derivedFrom":makeQuery(id+"F6.opPattern","COPY",BODY,{"derivedFrom":makeQuery(id+"F4.opPattern","COPY",BODY,{"derivedFrom":makeQuery(id+"F2.opPattern","COPY",BODY,{"derivedFrom":makeQuery(id+"F1.opRevolve","SWEPT_BODY",BODY,{"disambiguationData":[OSD([sQuery(id+"F0.wireOp",EDGE,"E1")])]}),"instanceName":"1"}),"instanceName":"1"}),"instanceName":"1"}),"instanceName":"1"});
            var Q113;
            Q113=makeQuery(id+"F9.opPattern","COPY",BODY,{"derivedFrom":makeQuery(id+"F6.opPattern","COPY",BODY,{"derivedFrom":makeQuery(id+"F4.opPattern","COPY",BODY,{"derivedFrom":makeQuery(id+"F3.opPattern","COPY",BODY,{"derivedFrom":makeQuery(id+"F2.opPattern","COPY",BODY,{"derivedFrom":makeQuery(id+"F1.opRevolve","SWEPT_BODY",BODY,{"disambiguationData":[OSD([sQuery(id+"F0.wireOp",EDGE,"E1")])]}),"instanceName":"1"}),"instanceName":"1"}),"instanceName":"1"}),"instanceName":"1"}),"instanceName":"1"});
            var Q114;
            Q114=makeQuery(id+"F9.opPattern","COPY",BODY,{"derivedFrom":makeQuery(id+"F6.opPattern","COPY",BODY,{"derivedFrom":makeQuery(id+"F5.opPattern","COPY",BODY,{"derivedFrom":makeQuery(id+"F1.opRevolve","SWEPT_BODY",BODY,{"disambiguationData":[OSD([sQuery(id+"F0.wireOp",EDGE,"E1")])]}),"instanceName":"1"}),"instanceName":"1"}),"instanceName":"1"});
            var Q115;
            Q115=makeQuery(id+"F9.opPattern","COPY",BODY,{"derivedFrom":makeQuery(id+"F6.opPattern","COPY",BODY,{"derivedFrom":makeQuery(id+"F5.opPattern","COPY",BODY,{"derivedFrom":makeQuery(id+"F2.opPattern","COPY",BODY,{"derivedFrom":makeQuery(id+"F1.opRevolve","SWEPT_BODY",BODY,{"disambiguationData":[OSD([sQuery(id+"F0.wireOp",EDGE,"E1")])]}),"instanceName":"1"}),"instanceName":"1"}),"instanceName":"1"}),"instanceName":"1"});
            var Q116;
            Q116=makeQuery(id+"F9.opPattern","COPY",BODY,{"derivedFrom":makeQuery(id+"F6.opPattern","COPY",BODY,{"derivedFrom":makeQuery(id+"F5.opPattern","COPY",BODY,{"derivedFrom":makeQuery(id+"F3.opPattern","COPY",BODY,{"derivedFrom":makeQuery(id+"F2.opPattern","COPY",BODY,{"derivedFrom":makeQuery(id+"F1.opRevolve","SWEPT_BODY",BODY,{"disambiguationData":[OSD([sQuery(id+"F0.wireOp",EDGE,"E1")])]}),"instanceName":"1"}),"instanceName":"1"}),"instanceName":"1"}),"instanceName":"1"}),"instanceName":"1"});
            var Q117;
            Q117=makeQuery(id+"F9.opPattern","COPY",BODY,{"derivedFrom":makeQuery(id+"F6.opPattern","COPY",BODY,{"derivedFrom":makeQuery(id+"F5.opPattern","COPY",BODY,{"derivedFrom":makeQuery(id+"F4.opPattern","COPY",BODY,{"derivedFrom":makeQuery(id+"F1.opRevolve","SWEPT_BODY",BODY,{"disambiguationData":[OSD([sQuery(id+"F0.wireOp",EDGE,"E1")])]}),"instanceName":"1"}),"instanceName":"1"}),"instanceName":"1"}),"instanceName":"1"});
            var Q118;
            Q118=makeQuery(id+"F9.opPattern","COPY",BODY,{"derivedFrom":makeQuery(id+"F6.opPattern","COPY",BODY,{"derivedFrom":makeQuery(id+"F5.opPattern","COPY",BODY,{"derivedFrom":makeQuery(id+"F4.opPattern","COPY",BODY,{"derivedFrom":makeQuery(id+"F2.opPattern","COPY",BODY,{"derivedFrom":makeQuery(id+"F1.opRevolve","SWEPT_BODY",BODY,{"disambiguationData":[OSD([sQuery(id+"F0.wireOp",EDGE,"E1")])]}),"instanceName":"1"}),"instanceName":"1"}),"instanceName":"1"}),"instanceName":"1"}),"instanceName":"1"});
            var Q119;
            Q119=makeQuery(id+"F9.opPattern","COPY",BODY,{"derivedFrom":makeQuery(id+"F6.opPattern","COPY",BODY,{"derivedFrom":makeQuery(id+"F5.opPattern","COPY",BODY,{"derivedFrom":makeQuery(id+"F4.opPattern","COPY",BODY,{"derivedFrom":makeQuery(id+"F3.opPattern","COPY",BODY,{"derivedFrom":makeQuery(id+"F2.opPattern","COPY",BODY,{"derivedFrom":makeQuery(id+"F1.opRevolve","SWEPT_BODY",BODY,{"disambiguationData":[OSD([sQuery(id+"F0.wireOp",EDGE,"E1")])]}),"instanceName":"1"}),"instanceName":"1"}),"instanceName":"1"}),"instanceName":"1"}),"instanceName":"1"}),"instanceName":"1"});
            var Q120;
            Q120=makeQuery(id+"F9.opPattern","COPY",BODY,{"derivedFrom":makeQuery(id+"F7.opPattern","COPY",BODY,{"derivedFrom":makeQuery(id+"F1.opRevolve","SWEPT_BODY",BODY,{"disambiguationData":[OSD([sQuery(id+"F0.wireOp",EDGE,"E1")])]}),"instanceName":"1"}),"instanceName":"1"});
            var Q121;
            Q121=makeQuery(id+"F9.opPattern","COPY",BODY,{"derivedFrom":makeQuery(id+"F7.opPattern","COPY",BODY,{"derivedFrom":makeQuery(id+"F2.opPattern","COPY",BODY,{"derivedFrom":makeQuery(id+"F1.opRevolve","SWEPT_BODY",BODY,{"disambiguationData":[OSD([sQuery(id+"F0.wireOp",EDGE,"E1")])]}),"instanceName":"1"}),"instanceName":"1"}),"instanceName":"1"});
            var Q122;
            Q122=makeQuery(id+"F9.opPattern","COPY",BODY,{"derivedFrom":makeQuery(id+"F7.opPattern","COPY",BODY,{"derivedFrom":makeQuery(id+"F3.opPattern","COPY",BODY,{"derivedFrom":makeQuery(id+"F2.opPattern","COPY",BODY,{"derivedFrom":makeQuery(id+"F1.opRevolve","SWEPT_BODY",BODY,{"disambiguationData":[OSD([sQuery(id+"F0.wireOp",EDGE,"E1")])]}),"instanceName":"1"}),"instanceName":"1"}),"instanceName":"1"}),"instanceName":"1"});
            var Q123;
            Q123=makeQuery(id+"F9.opPattern","COPY",BODY,{"derivedFrom":makeQuery(id+"F7.opPattern","COPY",BODY,{"derivedFrom":makeQuery(id+"F4.opPattern","COPY",BODY,{"derivedFrom":makeQuery(id+"F1.opRevolve","SWEPT_BODY",BODY,{"disambiguationData":[OSD([sQuery(id+"F0.wireOp",EDGE,"E1")])]}),"instanceName":"1"}),"instanceName":"1"}),"instanceName":"1"});
            var Q124;
            Q124=makeQuery(id+"F9.opPattern","COPY",BODY,{"derivedFrom":makeQuery(id+"F7.opPattern","COPY",BODY,{"derivedFrom":makeQuery(id+"F4.opPattern","COPY",BODY,{"derivedFrom":makeQuery(id+"F2.opPattern","COPY",BODY,{"derivedFrom":makeQuery(id+"F1.opRevolve","SWEPT_BODY",BODY,{"disambiguationData":[OSD([sQuery(id+"F0.wireOp",EDGE,"E1")])]}),"instanceName":"1"}),"instanceName":"1"}),"instanceName":"1"}),"instanceName":"1"});
            var Q125;
            Q125=makeQuery(id+"F9.opPattern","COPY",BODY,{"derivedFrom":makeQuery(id+"F7.opPattern","COPY",BODY,{"derivedFrom":makeQuery(id+"F4.opPattern","COPY",BODY,{"derivedFrom":makeQuery(id+"F3.opPattern","COPY",BODY,{"derivedFrom":makeQuery(id+"F2.opPattern","COPY",BODY,{"derivedFrom":makeQuery(id+"F1.opRevolve","SWEPT_BODY",BODY,{"disambiguationData":[OSD([sQuery(id+"F0.wireOp",EDGE,"E1")])]}),"instanceName":"1"}),"instanceName":"1"}),"instanceName":"1"}),"instanceName":"1"}),"instanceName":"1"});
            var Q126;
            Q126=makeQuery(id+"F9.opPattern","COPY",BODY,{"derivedFrom":makeQuery(id+"F7.opPattern","COPY",BODY,{"derivedFrom":makeQuery(id+"F5.opPattern","COPY",BODY,{"derivedFrom":makeQuery(id+"F1.opRevolve","SWEPT_BODY",BODY,{"disambiguationData":[OSD([sQuery(id+"F0.wireOp",EDGE,"E1")])]}),"instanceName":"1"}),"instanceName":"1"}),"instanceName":"1"});
            var Q127;
            Q127=makeQuery(id+"F9.opPattern","COPY",BODY,{"derivedFrom":makeQuery(id+"F7.opPattern","COPY",BODY,{"derivedFrom":makeQuery(id+"F5.opPattern","COPY",BODY,{"derivedFrom":makeQuery(id+"F2.opPattern","COPY",BODY,{"derivedFrom":makeQuery(id+"F1.opRevolve","SWEPT_BODY",BODY,{"disambiguationData":[OSD([sQuery(id+"F0.wireOp",EDGE,"E1")])]}),"instanceName":"1"}),"instanceName":"1"}),"instanceName":"1"}),"instanceName":"1"});
            var Q128;
            Q128=makeQuery(id+"F9.opPattern","COPY",BODY,{"derivedFrom":makeQuery(id+"F7.opPattern","COPY",BODY,{"derivedFrom":makeQuery(id+"F5.opPattern","COPY",BODY,{"derivedFrom":makeQuery(id+"F3.opPattern","COPY",BODY,{"derivedFrom":makeQuery(id+"F2.opPattern","COPY",BODY,{"derivedFrom":makeQuery(id+"F1.opRevolve","SWEPT_BODY",BODY,{"disambiguationData":[OSD([sQuery(id+"F0.wireOp",EDGE,"E1")])]}),"instanceName":"1"}),"instanceName":"1"}),"instanceName":"1"}),"instanceName":"1"}),"instanceName":"1"});
            var Q129;
            Q129=makeQuery(id+"F9.opPattern","COPY",BODY,{"derivedFrom":makeQuery(id+"F7.opPattern","COPY",BODY,{"derivedFrom":makeQuery(id+"F5.opPattern","COPY",BODY,{"derivedFrom":makeQuery(id+"F4.opPattern","COPY",BODY,{"derivedFrom":makeQuery(id+"F1.opRevolve","SWEPT_BODY",BODY,{"disambiguationData":[OSD([sQuery(id+"F0.wireOp",EDGE,"E1")])]}),"instanceName":"1"}),"instanceName":"1"}),"instanceName":"1"}),"instanceName":"1"});
            var Q130;
            Q130=makeQuery(id+"F9.opPattern","COPY",BODY,{"derivedFrom":makeQuery(id+"F7.opPattern","COPY",BODY,{"derivedFrom":makeQuery(id+"F5.opPattern","COPY",BODY,{"derivedFrom":makeQuery(id+"F4.opPattern","COPY",BODY,{"derivedFrom":makeQuery(id+"F2.opPattern","COPY",BODY,{"derivedFrom":makeQuery(id+"F1.opRevolve","SWEPT_BODY",BODY,{"disambiguationData":[OSD([sQuery(id+"F0.wireOp",EDGE,"E1")])]}),"instanceName":"1"}),"instanceName":"1"}),"instanceName":"1"}),"instanceName":"1"}),"instanceName":"1"});
            var Q131;
            Q131=makeQuery(id+"F9.opPattern","COPY",BODY,{"derivedFrom":makeQuery(id+"F7.opPattern","COPY",BODY,{"derivedFrom":makeQuery(id+"F5.opPattern","COPY",BODY,{"derivedFrom":makeQuery(id+"F4.opPattern","COPY",BODY,{"derivedFrom":makeQuery(id+"F3.opPattern","COPY",BODY,{"derivedFrom":makeQuery(id+"F2.opPattern","COPY",BODY,{"derivedFrom":makeQuery(id+"F1.opRevolve","SWEPT_BODY",BODY,{"disambiguationData":[OSD([sQuery(id+"F0.wireOp",EDGE,"E1")])]}),"instanceName":"1"}),"instanceName":"1"}),"instanceName":"1"}),"instanceName":"1"}),"instanceName":"1"}),"instanceName":"1"});
            var Q132;
            Q132=makeQuery(id+"F9.opPattern","COPY",BODY,{"derivedFrom":makeQuery(id+"F7.opPattern","COPY",BODY,{"derivedFrom":makeQuery(id+"F6.opPattern","COPY",BODY,{"derivedFrom":makeQuery(id+"F1.opRevolve","SWEPT_BODY",BODY,{"disambiguationData":[OSD([sQuery(id+"F0.wireOp",EDGE,"E1")])]}),"instanceName":"1"}),"instanceName":"1"}),"instanceName":"1"});
            var Q133;
            Q133=makeQuery(id+"F9.opPattern","COPY",BODY,{"derivedFrom":makeQuery(id+"F7.opPattern","COPY",BODY,{"derivedFrom":makeQuery(id+"F6.opPattern","COPY",BODY,{"derivedFrom":makeQuery(id+"F2.opPattern","COPY",BODY,{"derivedFrom":makeQuery(id+"F1.opRevolve","SWEPT_BODY",BODY,{"disambiguationData":[OSD([sQuery(id+"F0.wireOp",EDGE,"E1")])]}),"instanceName":"1"}),"instanceName":"1"}),"instanceName":"1"}),"instanceName":"1"});
            var Q134;
            Q134=makeQuery(id+"F9.opPattern","COPY",BODY,{"derivedFrom":makeQuery(id+"F7.opPattern","COPY",BODY,{"derivedFrom":makeQuery(id+"F6.opPattern","COPY",BODY,{"derivedFrom":makeQuery(id+"F3.opPattern","COPY",BODY,{"derivedFrom":makeQuery(id+"F2.opPattern","COPY",BODY,{"derivedFrom":makeQuery(id+"F1.opRevolve","SWEPT_BODY",BODY,{"disambiguationData":[OSD([sQuery(id+"F0.wireOp",EDGE,"E1")])]}),"instanceName":"1"}),"instanceName":"1"}),"instanceName":"1"}),"instanceName":"1"}),"instanceName":"1"});
            var Q135;
            Q135=makeQuery(id+"F9.opPattern","COPY",BODY,{"derivedFrom":makeQuery(id+"F7.opPattern","COPY",BODY,{"derivedFrom":makeQuery(id+"F6.opPattern","COPY",BODY,{"derivedFrom":makeQuery(id+"F4.opPattern","COPY",BODY,{"derivedFrom":makeQuery(id+"F1.opRevolve","SWEPT_BODY",BODY,{"disambiguationData":[OSD([sQuery(id+"F0.wireOp",EDGE,"E1")])]}),"instanceName":"1"}),"instanceName":"1"}),"instanceName":"1"}),"instanceName":"1"});
            var Q136;
            Q136=makeQuery(id+"F9.opPattern","COPY",BODY,{"derivedFrom":makeQuery(id+"F7.opPattern","COPY",BODY,{"derivedFrom":makeQuery(id+"F6.opPattern","COPY",BODY,{"derivedFrom":makeQuery(id+"F4.opPattern","COPY",BODY,{"derivedFrom":makeQuery(id+"F2.opPattern","COPY",BODY,{"derivedFrom":makeQuery(id+"F1.opRevolve","SWEPT_BODY",BODY,{"disambiguationData":[OSD([sQuery(id+"F0.wireOp",EDGE,"E1")])]}),"instanceName":"1"}),"instanceName":"1"}),"instanceName":"1"}),"instanceName":"1"}),"instanceName":"1"});
            var Q137;
            Q137=makeQuery(id+"F9.opPattern","COPY",BODY,{"derivedFrom":makeQuery(id+"F7.opPattern","COPY",BODY,{"derivedFrom":makeQuery(id+"F6.opPattern","COPY",BODY,{"derivedFrom":makeQuery(id+"F4.opPattern","COPY",BODY,{"derivedFrom":makeQuery(id+"F3.opPattern","COPY",BODY,{"derivedFrom":makeQuery(id+"F2.opPattern","COPY",BODY,{"derivedFrom":makeQuery(id+"F1.opRevolve","SWEPT_BODY",BODY,{"disambiguationData":[OSD([sQuery(id+"F0.wireOp",EDGE,"E1")])]}),"instanceName":"1"}),"instanceName":"1"}),"instanceName":"1"}),"instanceName":"1"}),"instanceName":"1"}),"instanceName":"1"});
            var Q138;
            Q138=makeQuery(id+"F9.opPattern","COPY",BODY,{"derivedFrom":makeQuery(id+"F7.opPattern","COPY",BODY,{"derivedFrom":makeQuery(id+"F6.opPattern","COPY",BODY,{"derivedFrom":makeQuery(id+"F5.opPattern","COPY",BODY,{"derivedFrom":makeQuery(id+"F1.opRevolve","SWEPT_BODY",BODY,{"disambiguationData":[OSD([sQuery(id+"F0.wireOp",EDGE,"E1")])]}),"instanceName":"1"}),"instanceName":"1"}),"instanceName":"1"}),"instanceName":"1"});
            var Q139;
            Q139=makeQuery(id+"F9.opPattern","COPY",BODY,{"derivedFrom":makeQuery(id+"F7.opPattern","COPY",BODY,{"derivedFrom":makeQuery(id+"F6.opPattern","COPY",BODY,{"derivedFrom":makeQuery(id+"F5.opPattern","COPY",BODY,{"derivedFrom":makeQuery(id+"F2.opPattern","COPY",BODY,{"derivedFrom":makeQuery(id+"F1.opRevolve","SWEPT_BODY",BODY,{"disambiguationData":[OSD([sQuery(id+"F0.wireOp",EDGE,"E1")])]}),"instanceName":"1"}),"instanceName":"1"}),"instanceName":"1"}),"instanceName":"1"}),"instanceName":"1"});
            var Q140;
            Q140=makeQuery(id+"F9.opPattern","COPY",BODY,{"derivedFrom":makeQuery(id+"F7.opPattern","COPY",BODY,{"derivedFrom":makeQuery(id+"F6.opPattern","COPY",BODY,{"derivedFrom":makeQuery(id+"F5.opPattern","COPY",BODY,{"derivedFrom":makeQuery(id+"F3.opPattern","COPY",BODY,{"derivedFrom":makeQuery(id+"F2.opPattern","COPY",BODY,{"derivedFrom":makeQuery(id+"F1.opRevolve","SWEPT_BODY",BODY,{"disambiguationData":[OSD([sQuery(id+"F0.wireOp",EDGE,"E1")])]}),"instanceName":"1"}),"instanceName":"1"}),"instanceName":"1"}),"instanceName":"1"}),"instanceName":"1"}),"instanceName":"1"});
            var Q141;
            Q141=makeQuery(id+"F9.opPattern","COPY",BODY,{"derivedFrom":makeQuery(id+"F7.opPattern","COPY",BODY,{"derivedFrom":makeQuery(id+"F6.opPattern","COPY",BODY,{"derivedFrom":makeQuery(id+"F5.opPattern","COPY",BODY,{"derivedFrom":makeQuery(id+"F4.opPattern","COPY",BODY,{"derivedFrom":makeQuery(id+"F1.opRevolve","SWEPT_BODY",BODY,{"disambiguationData":[OSD([sQuery(id+"F0.wireOp",EDGE,"E1")])]}),"instanceName":"1"}),"instanceName":"1"}),"instanceName":"1"}),"instanceName":"1"}),"instanceName":"1"});
            var Q142;
            Q142=makeQuery(id+"F9.opPattern","COPY",BODY,{"derivedFrom":makeQuery(id+"F7.opPattern","COPY",BODY,{"derivedFrom":makeQuery(id+"F6.opPattern","COPY",BODY,{"derivedFrom":makeQuery(id+"F5.opPattern","COPY",BODY,{"derivedFrom":makeQuery(id+"F4.opPattern","COPY",BODY,{"derivedFrom":makeQuery(id+"F2.opPattern","COPY",BODY,{"derivedFrom":makeQuery(id+"F1.opRevolve","SWEPT_BODY",BODY,{"disambiguationData":[OSD([sQuery(id+"F0.wireOp",EDGE,"E1")])]}),"instanceName":"1"}),"instanceName":"1"}),"instanceName":"1"}),"instanceName":"1"}),"instanceName":"1"}),"instanceName":"1"});
            var Q143;
            Q143=makeQuery(id+"F9.opPattern","COPY",BODY,{"derivedFrom":makeQuery(id+"F7.opPattern","COPY",BODY,{"derivedFrom":makeQuery(id+"F6.opPattern","COPY",BODY,{"derivedFrom":makeQuery(id+"F5.opPattern","COPY",BODY,{"derivedFrom":makeQuery(id+"F4.opPattern","COPY",BODY,{"derivedFrom":makeQuery(id+"F3.opPattern","COPY",BODY,{"derivedFrom":makeQuery(id+"F2.opPattern","COPY",BODY,{"derivedFrom":makeQuery(id+"F1.opRevolve","SWEPT_BODY",BODY,{"disambiguationData":[OSD([sQuery(id+"F0.wireOp",EDGE,"E1")])]}),"instanceName":"1"}),"instanceName":"1"}),"instanceName":"1"}),"instanceName":"1"}),"instanceName":"1"}),"instanceName":"1"}),"instanceName":"1"});
            var Q144;
            Q144=makeQuery(id+"F9.opPattern","COPY",BODY,{"derivedFrom":makeQuery(id+"F8.opPattern","COPY",BODY,{"derivedFrom":makeQuery(id+"F1.opRevolve","SWEPT_BODY",BODY,{"disambiguationData":[OSD([sQuery(id+"F0.wireOp",EDGE,"E1")])]}),"instanceName":"1"}),"instanceName":"1"});
            var Q145;
            Q145=makeQuery(id+"F9.opPattern","COPY",BODY,{"derivedFrom":makeQuery(id+"F8.opPattern","COPY",BODY,{"derivedFrom":makeQuery(id+"F2.opPattern","COPY",BODY,{"derivedFrom":makeQuery(id+"F1.opRevolve","SWEPT_BODY",BODY,{"disambiguationData":[OSD([sQuery(id+"F0.wireOp",EDGE,"E1")])]}),"instanceName":"1"}),"instanceName":"1"}),"instanceName":"1"});
            var Q146;
            Q146=makeQuery(id+"F9.opPattern","COPY",BODY,{"derivedFrom":makeQuery(id+"F8.opPattern","COPY",BODY,{"derivedFrom":makeQuery(id+"F3.opPattern","COPY",BODY,{"derivedFrom":makeQuery(id+"F2.opPattern","COPY",BODY,{"derivedFrom":makeQuery(id+"F1.opRevolve","SWEPT_BODY",BODY,{"disambiguationData":[OSD([sQuery(id+"F0.wireOp",EDGE,"E1")])]}),"instanceName":"1"}),"instanceName":"1"}),"instanceName":"1"}),"instanceName":"1"});
            var Q147;
            Q147=makeQuery(id+"F9.opPattern","COPY",BODY,{"derivedFrom":makeQuery(id+"F8.opPattern","COPY",BODY,{"derivedFrom":makeQuery(id+"F4.opPattern","COPY",BODY,{"derivedFrom":makeQuery(id+"F1.opRevolve","SWEPT_BODY",BODY,{"disambiguationData":[OSD([sQuery(id+"F0.wireOp",EDGE,"E1")])]}),"instanceName":"1"}),"instanceName":"1"}),"instanceName":"1"});
            var Q148;
            Q148=makeQuery(id+"F9.opPattern","COPY",BODY,{"derivedFrom":makeQuery(id+"F8.opPattern","COPY",BODY,{"derivedFrom":makeQuery(id+"F4.opPattern","COPY",BODY,{"derivedFrom":makeQuery(id+"F2.opPattern","COPY",BODY,{"derivedFrom":makeQuery(id+"F1.opRevolve","SWEPT_BODY",BODY,{"disambiguationData":[OSD([sQuery(id+"F0.wireOp",EDGE,"E1")])]}),"instanceName":"1"}),"instanceName":"1"}),"instanceName":"1"}),"instanceName":"1"});
            var Q149;
            Q149=makeQuery(id+"F9.opPattern","COPY",BODY,{"derivedFrom":makeQuery(id+"F8.opPattern","COPY",BODY,{"derivedFrom":makeQuery(id+"F4.opPattern","COPY",BODY,{"derivedFrom":makeQuery(id+"F3.opPattern","COPY",BODY,{"derivedFrom":makeQuery(id+"F2.opPattern","COPY",BODY,{"derivedFrom":makeQuery(id+"F1.opRevolve","SWEPT_BODY",BODY,{"disambiguationData":[OSD([sQuery(id+"F0.wireOp",EDGE,"E1")])]}),"instanceName":"1"}),"instanceName":"1"}),"instanceName":"1"}),"instanceName":"1"}),"instanceName":"1"});
            var Q150;
            Q150=makeQuery(id+"F9.opPattern","COPY",BODY,{"derivedFrom":makeQuery(id+"F8.opPattern","COPY",BODY,{"derivedFrom":makeQuery(id+"F5.opPattern","COPY",BODY,{"derivedFrom":makeQuery(id+"F1.opRevolve","SWEPT_BODY",BODY,{"disambiguationData":[OSD([sQuery(id+"F0.wireOp",EDGE,"E1")])]}),"instanceName":"1"}),"instanceName":"1"}),"instanceName":"1"});
            var Q151;
            Q151=makeQuery(id+"F9.opPattern","COPY",BODY,{"derivedFrom":makeQuery(id+"F8.opPattern","COPY",BODY,{"derivedFrom":makeQuery(id+"F5.opPattern","COPY",BODY,{"derivedFrom":makeQuery(id+"F2.opPattern","COPY",BODY,{"derivedFrom":makeQuery(id+"F1.opRevolve","SWEPT_BODY",BODY,{"disambiguationData":[OSD([sQuery(id+"F0.wireOp",EDGE,"E1")])]}),"instanceName":"1"}),"instanceName":"1"}),"instanceName":"1"}),"instanceName":"1"});
            var Q152;
            Q152=makeQuery(id+"F9.opPattern","COPY",BODY,{"derivedFrom":makeQuery(id+"F8.opPattern","COPY",BODY,{"derivedFrom":makeQuery(id+"F5.opPattern","COPY",BODY,{"derivedFrom":makeQuery(id+"F3.opPattern","COPY",BODY,{"derivedFrom":makeQuery(id+"F2.opPattern","COPY",BODY,{"derivedFrom":makeQuery(id+"F1.opRevolve","SWEPT_BODY",BODY,{"disambiguationData":[OSD([sQuery(id+"F0.wireOp",EDGE,"E1")])]}),"instanceName":"1"}),"instanceName":"1"}),"instanceName":"1"}),"instanceName":"1"}),"instanceName":"1"});
            var Q153;
            Q153=makeQuery(id+"F9.opPattern","COPY",BODY,{"derivedFrom":makeQuery(id+"F8.opPattern","COPY",BODY,{"derivedFrom":makeQuery(id+"F5.opPattern","COPY",BODY,{"derivedFrom":makeQuery(id+"F4.opPattern","COPY",BODY,{"derivedFrom":makeQuery(id+"F1.opRevolve","SWEPT_BODY",BODY,{"disambiguationData":[OSD([sQuery(id+"F0.wireOp",EDGE,"E1")])]}),"instanceName":"1"}),"instanceName":"1"}),"instanceName":"1"}),"instanceName":"1"});
            var Q154;
            Q154=makeQuery(id+"F9.opPattern","COPY",BODY,{"derivedFrom":makeQuery(id+"F8.opPattern","COPY",BODY,{"derivedFrom":makeQuery(id+"F5.opPattern","COPY",BODY,{"derivedFrom":makeQuery(id+"F4.opPattern","COPY",BODY,{"derivedFrom":makeQuery(id+"F2.opPattern","COPY",BODY,{"derivedFrom":makeQuery(id+"F1.opRevolve","SWEPT_BODY",BODY,{"disambiguationData":[OSD([sQuery(id+"F0.wireOp",EDGE,"E1")])]}),"instanceName":"1"}),"instanceName":"1"}),"instanceName":"1"}),"instanceName":"1"}),"instanceName":"1"});
            var Q155;
            Q155=makeQuery(id+"F9.opPattern","COPY",BODY,{"derivedFrom":makeQuery(id+"F8.opPattern","COPY",BODY,{"derivedFrom":makeQuery(id+"F5.opPattern","COPY",BODY,{"derivedFrom":makeQuery(id+"F4.opPattern","COPY",BODY,{"derivedFrom":makeQuery(id+"F3.opPattern","COPY",BODY,{"derivedFrom":makeQuery(id+"F2.opPattern","COPY",BODY,{"derivedFrom":makeQuery(id+"F1.opRevolve","SWEPT_BODY",BODY,{"disambiguationData":[OSD([sQuery(id+"F0.wireOp",EDGE,"E1")])]}),"instanceName":"1"}),"instanceName":"1"}),"instanceName":"1"}),"instanceName":"1"}),"instanceName":"1"}),"instanceName":"1"});
            var Q156;
            Q156=makeQuery(id+"F9.opPattern","COPY",BODY,{"derivedFrom":makeQuery(id+"F8.opPattern","COPY",BODY,{"derivedFrom":makeQuery(id+"F6.opPattern","COPY",BODY,{"derivedFrom":makeQuery(id+"F1.opRevolve","SWEPT_BODY",BODY,{"disambiguationData":[OSD([sQuery(id+"F0.wireOp",EDGE,"E1")])]}),"instanceName":"1"}),"instanceName":"1"}),"instanceName":"1"});
            var Q157;
            Q157=makeQuery(id+"F9.opPattern","COPY",BODY,{"derivedFrom":makeQuery(id+"F8.opPattern","COPY",BODY,{"derivedFrom":makeQuery(id+"F6.opPattern","COPY",BODY,{"derivedFrom":makeQuery(id+"F2.opPattern","COPY",BODY,{"derivedFrom":makeQuery(id+"F1.opRevolve","SWEPT_BODY",BODY,{"disambiguationData":[OSD([sQuery(id+"F0.wireOp",EDGE,"E1")])]}),"instanceName":"1"}),"instanceName":"1"}),"instanceName":"1"}),"instanceName":"1"});
            var Q158;
            Q158=makeQuery(id+"F9.opPattern","COPY",BODY,{"derivedFrom":makeQuery(id+"F8.opPattern","COPY",BODY,{"derivedFrom":makeQuery(id+"F6.opPattern","COPY",BODY,{"derivedFrom":makeQuery(id+"F3.opPattern","COPY",BODY,{"derivedFrom":makeQuery(id+"F2.opPattern","COPY",BODY,{"derivedFrom":makeQuery(id+"F1.opRevolve","SWEPT_BODY",BODY,{"disambiguationData":[OSD([sQuery(id+"F0.wireOp",EDGE,"E1")])]}),"instanceName":"1"}),"instanceName":"1"}),"instanceName":"1"}),"instanceName":"1"}),"instanceName":"1"});
            var Q159;
            Q159=makeQuery(id+"F9.opPattern","COPY",BODY,{"derivedFrom":makeQuery(id+"F8.opPattern","COPY",BODY,{"derivedFrom":makeQuery(id+"F6.opPattern","COPY",BODY,{"derivedFrom":makeQuery(id+"F4.opPattern","COPY",BODY,{"derivedFrom":makeQuery(id+"F1.opRevolve","SWEPT_BODY",BODY,{"disambiguationData":[OSD([sQuery(id+"F0.wireOp",EDGE,"E1")])]}),"instanceName":"1"}),"instanceName":"1"}),"instanceName":"1"}),"instanceName":"1"});
            var Q160;
            Q160=makeQuery(id+"F9.opPattern","COPY",BODY,{"derivedFrom":makeQuery(id+"F8.opPattern","COPY",BODY,{"derivedFrom":makeQuery(id+"F6.opPattern","COPY",BODY,{"derivedFrom":makeQuery(id+"F4.opPattern","COPY",BODY,{"derivedFrom":makeQuery(id+"F2.opPattern","COPY",BODY,{"derivedFrom":makeQuery(id+"F1.opRevolve","SWEPT_BODY",BODY,{"disambiguationData":[OSD([sQuery(id+"F0.wireOp",EDGE,"E1")])]}),"instanceName":"1"}),"instanceName":"1"}),"instanceName":"1"}),"instanceName":"1"}),"instanceName":"1"});
            var Q161;
            Q161=makeQuery(id+"F9.opPattern","COPY",BODY,{"derivedFrom":makeQuery(id+"F8.opPattern","COPY",BODY,{"derivedFrom":makeQuery(id+"F6.opPattern","COPY",BODY,{"derivedFrom":makeQuery(id+"F4.opPattern","COPY",BODY,{"derivedFrom":makeQuery(id+"F3.opPattern","COPY",BODY,{"derivedFrom":makeQuery(id+"F2.opPattern","COPY",BODY,{"derivedFrom":makeQuery(id+"F1.opRevolve","SWEPT_BODY",BODY,{"disambiguationData":[OSD([sQuery(id+"F0.wireOp",EDGE,"E1")])]}),"instanceName":"1"}),"instanceName":"1"}),"instanceName":"1"}),"instanceName":"1"}),"instanceName":"1"}),"instanceName":"1"});
            var Q162;
            Q162=makeQuery(id+"F9.opPattern","COPY",BODY,{"derivedFrom":makeQuery(id+"F8.opPattern","COPY",BODY,{"derivedFrom":makeQuery(id+"F6.opPattern","COPY",BODY,{"derivedFrom":makeQuery(id+"F5.opPattern","COPY",BODY,{"derivedFrom":makeQuery(id+"F1.opRevolve","SWEPT_BODY",BODY,{"disambiguationData":[OSD([sQuery(id+"F0.wireOp",EDGE,"E1")])]}),"instanceName":"1"}),"instanceName":"1"}),"instanceName":"1"}),"instanceName":"1"});
            var Q163;
            Q163=makeQuery(id+"F9.opPattern","COPY",BODY,{"derivedFrom":makeQuery(id+"F8.opPattern","COPY",BODY,{"derivedFrom":makeQuery(id+"F6.opPattern","COPY",BODY,{"derivedFrom":makeQuery(id+"F5.opPattern","COPY",BODY,{"derivedFrom":makeQuery(id+"F2.opPattern","COPY",BODY,{"derivedFrom":makeQuery(id+"F1.opRevolve","SWEPT_BODY",BODY,{"disambiguationData":[OSD([sQuery(id+"F0.wireOp",EDGE,"E1")])]}),"instanceName":"1"}),"instanceName":"1"}),"instanceName":"1"}),"instanceName":"1"}),"instanceName":"1"});
            var Q164;
            Q164=makeQuery(id+"F9.opPattern","COPY",BODY,{"derivedFrom":makeQuery(id+"F8.opPattern","COPY",BODY,{"derivedFrom":makeQuery(id+"F6.opPattern","COPY",BODY,{"derivedFrom":makeQuery(id+"F5.opPattern","COPY",BODY,{"derivedFrom":makeQuery(id+"F3.opPattern","COPY",BODY,{"derivedFrom":makeQuery(id+"F2.opPattern","COPY",BODY,{"derivedFrom":makeQuery(id+"F1.opRevolve","SWEPT_BODY",BODY,{"disambiguationData":[OSD([sQuery(id+"F0.wireOp",EDGE,"E1")])]}),"instanceName":"1"}),"instanceName":"1"}),"instanceName":"1"}),"instanceName":"1"}),"instanceName":"1"}),"instanceName":"1"});
            var Q165;
            Q165=makeQuery(id+"F9.opPattern","COPY",BODY,{"derivedFrom":makeQuery(id+"F8.opPattern","COPY",BODY,{"derivedFrom":makeQuery(id+"F6.opPattern","COPY",BODY,{"derivedFrom":makeQuery(id+"F5.opPattern","COPY",BODY,{"derivedFrom":makeQuery(id+"F4.opPattern","COPY",BODY,{"derivedFrom":makeQuery(id+"F1.opRevolve","SWEPT_BODY",BODY,{"disambiguationData":[OSD([sQuery(id+"F0.wireOp",EDGE,"E1")])]}),"instanceName":"1"}),"instanceName":"1"}),"instanceName":"1"}),"instanceName":"1"}),"instanceName":"1"});
            var Q166;
            Q166=makeQuery(id+"F9.opPattern","COPY",BODY,{"derivedFrom":makeQuery(id+"F8.opPattern","COPY",BODY,{"derivedFrom":makeQuery(id+"F6.opPattern","COPY",BODY,{"derivedFrom":makeQuery(id+"F5.opPattern","COPY",BODY,{"derivedFrom":makeQuery(id+"F4.opPattern","COPY",BODY,{"derivedFrom":makeQuery(id+"F2.opPattern","COPY",BODY,{"derivedFrom":makeQuery(id+"F1.opRevolve","SWEPT_BODY",BODY,{"disambiguationData":[OSD([sQuery(id+"F0.wireOp",EDGE,"E1")])]}),"instanceName":"1"}),"instanceName":"1"}),"instanceName":"1"}),"instanceName":"1"}),"instanceName":"1"}),"instanceName":"1"});
            var Q167;
            Q167=makeQuery(id+"F9.opPattern","COPY",BODY,{"derivedFrom":makeQuery(id+"F8.opPattern","COPY",BODY,{"derivedFrom":makeQuery(id+"F6.opPattern","COPY",BODY,{"derivedFrom":makeQuery(id+"F5.opPattern","COPY",BODY,{"derivedFrom":makeQuery(id+"F4.opPattern","COPY",BODY,{"derivedFrom":makeQuery(id+"F3.opPattern","COPY",BODY,{"derivedFrom":makeQuery(id+"F2.opPattern","COPY",BODY,{"derivedFrom":makeQuery(id+"F1.opRevolve","SWEPT_BODY",BODY,{"disambiguationData":[OSD([sQuery(id+"F0.wireOp",EDGE,"E1")])]}),"instanceName":"1"}),"instanceName":"1"}),"instanceName":"1"}),"instanceName":"1"}),"instanceName":"1"}),"instanceName":"1"}),"instanceName":"1"});
            var Q168;
            Q168=makeQuery(id+"F9.opPattern","COPY",BODY,{"derivedFrom":makeQuery(id+"F8.opPattern","COPY",BODY,{"derivedFrom":makeQuery(id+"F7.opPattern","COPY",BODY,{"derivedFrom":makeQuery(id+"F1.opRevolve","SWEPT_BODY",BODY,{"disambiguationData":[OSD([sQuery(id+"F0.wireOp",EDGE,"E1")])]}),"instanceName":"1"}),"instanceName":"1"}),"instanceName":"1"});
            var Q169;
            Q169=makeQuery(id+"F9.opPattern","COPY",BODY,{"derivedFrom":makeQuery(id+"F8.opPattern","COPY",BODY,{"derivedFrom":makeQuery(id+"F7.opPattern","COPY",BODY,{"derivedFrom":makeQuery(id+"F2.opPattern","COPY",BODY,{"derivedFrom":makeQuery(id+"F1.opRevolve","SWEPT_BODY",BODY,{"disambiguationData":[OSD([sQuery(id+"F0.wireOp",EDGE,"E1")])]}),"instanceName":"1"}),"instanceName":"1"}),"instanceName":"1"}),"instanceName":"1"});
            var Q170;
            Q170=makeQuery(id+"F9.opPattern","COPY",BODY,{"derivedFrom":makeQuery(id+"F8.opPattern","COPY",BODY,{"derivedFrom":makeQuery(id+"F7.opPattern","COPY",BODY,{"derivedFrom":makeQuery(id+"F3.opPattern","COPY",BODY,{"derivedFrom":makeQuery(id+"F2.opPattern","COPY",BODY,{"derivedFrom":makeQuery(id+"F1.opRevolve","SWEPT_BODY",BODY,{"disambiguationData":[OSD([sQuery(id+"F0.wireOp",EDGE,"E1")])]}),"instanceName":"1"}),"instanceName":"1"}),"instanceName":"1"}),"instanceName":"1"}),"instanceName":"1"});
            var Q171;
            Q171=makeQuery(id+"F9.opPattern","COPY",BODY,{"derivedFrom":makeQuery(id+"F8.opPattern","COPY",BODY,{"derivedFrom":makeQuery(id+"F7.opPattern","COPY",BODY,{"derivedFrom":makeQuery(id+"F4.opPattern","COPY",BODY,{"derivedFrom":makeQuery(id+"F1.opRevolve","SWEPT_BODY",BODY,{"disambiguationData":[OSD([sQuery(id+"F0.wireOp",EDGE,"E1")])]}),"instanceName":"1"}),"instanceName":"1"}),"instanceName":"1"}),"instanceName":"1"});
            var Q172;
            Q172=makeQuery(id+"F9.opPattern","COPY",BODY,{"derivedFrom":makeQuery(id+"F8.opPattern","COPY",BODY,{"derivedFrom":makeQuery(id+"F7.opPattern","COPY",BODY,{"derivedFrom":makeQuery(id+"F4.opPattern","COPY",BODY,{"derivedFrom":makeQuery(id+"F2.opPattern","COPY",BODY,{"derivedFrom":makeQuery(id+"F1.opRevolve","SWEPT_BODY",BODY,{"disambiguationData":[OSD([sQuery(id+"F0.wireOp",EDGE,"E1")])]}),"instanceName":"1"}),"instanceName":"1"}),"instanceName":"1"}),"instanceName":"1"}),"instanceName":"1"});
            var Q173;
            Q173=makeQuery(id+"F9.opPattern","COPY",BODY,{"derivedFrom":makeQuery(id+"F8.opPattern","COPY",BODY,{"derivedFrom":makeQuery(id+"F7.opPattern","COPY",BODY,{"derivedFrom":makeQuery(id+"F4.opPattern","COPY",BODY,{"derivedFrom":makeQuery(id+"F3.opPattern","COPY",BODY,{"derivedFrom":makeQuery(id+"F2.opPattern","COPY",BODY,{"derivedFrom":makeQuery(id+"F1.opRevolve","SWEPT_BODY",BODY,{"disambiguationData":[OSD([sQuery(id+"F0.wireOp",EDGE,"E1")])]}),"instanceName":"1"}),"instanceName":"1"}),"instanceName":"1"}),"instanceName":"1"}),"instanceName":"1"}),"instanceName":"1"});
            var Q174;
            Q174=makeQuery(id+"F9.opPattern","COPY",BODY,{"derivedFrom":makeQuery(id+"F8.opPattern","COPY",BODY,{"derivedFrom":makeQuery(id+"F7.opPattern","COPY",BODY,{"derivedFrom":makeQuery(id+"F5.opPattern","COPY",BODY,{"derivedFrom":makeQuery(id+"F1.opRevolve","SWEPT_BODY",BODY,{"disambiguationData":[OSD([sQuery(id+"F0.wireOp",EDGE,"E1")])]}),"instanceName":"1"}),"instanceName":"1"}),"instanceName":"1"}),"instanceName":"1"});
            var Q175;
            Q175=makeQuery(id+"F9.opPattern","COPY",BODY,{"derivedFrom":makeQuery(id+"F8.opPattern","COPY",BODY,{"derivedFrom":makeQuery(id+"F7.opPattern","COPY",BODY,{"derivedFrom":makeQuery(id+"F5.opPattern","COPY",BODY,{"derivedFrom":makeQuery(id+"F2.opPattern","COPY",BODY,{"derivedFrom":makeQuery(id+"F1.opRevolve","SWEPT_BODY",BODY,{"disambiguationData":[OSD([sQuery(id+"F0.wireOp",EDGE,"E1")])]}),"instanceName":"1"}),"instanceName":"1"}),"instanceName":"1"}),"instanceName":"1"}),"instanceName":"1"});
            var Q176;
            Q176=makeQuery(id+"F9.opPattern","COPY",BODY,{"derivedFrom":makeQuery(id+"F8.opPattern","COPY",BODY,{"derivedFrom":makeQuery(id+"F7.opPattern","COPY",BODY,{"derivedFrom":makeQuery(id+"F5.opPattern","COPY",BODY,{"derivedFrom":makeQuery(id+"F3.opPattern","COPY",BODY,{"derivedFrom":makeQuery(id+"F2.opPattern","COPY",BODY,{"derivedFrom":makeQuery(id+"F1.opRevolve","SWEPT_BODY",BODY,{"disambiguationData":[OSD([sQuery(id+"F0.wireOp",EDGE,"E1")])]}),"instanceName":"1"}),"instanceName":"1"}),"instanceName":"1"}),"instanceName":"1"}),"instanceName":"1"}),"instanceName":"1"});
            var Q177;
            Q177=makeQuery(id+"F9.opPattern","COPY",BODY,{"derivedFrom":makeQuery(id+"F8.opPattern","COPY",BODY,{"derivedFrom":makeQuery(id+"F7.opPattern","COPY",BODY,{"derivedFrom":makeQuery(id+"F5.opPattern","COPY",BODY,{"derivedFrom":makeQuery(id+"F4.opPattern","COPY",BODY,{"derivedFrom":makeQuery(id+"F1.opRevolve","SWEPT_BODY",BODY,{"disambiguationData":[OSD([sQuery(id+"F0.wireOp",EDGE,"E1")])]}),"instanceName":"1"}),"instanceName":"1"}),"instanceName":"1"}),"instanceName":"1"}),"instanceName":"1"});
            var Q178;
            Q178=makeQuery(id+"F9.opPattern","COPY",BODY,{"derivedFrom":makeQuery(id+"F8.opPattern","COPY",BODY,{"derivedFrom":makeQuery(id+"F7.opPattern","COPY",BODY,{"derivedFrom":makeQuery(id+"F5.opPattern","COPY",BODY,{"derivedFrom":makeQuery(id+"F4.opPattern","COPY",BODY,{"derivedFrom":makeQuery(id+"F2.opPattern","COPY",BODY,{"derivedFrom":makeQuery(id+"F1.opRevolve","SWEPT_BODY",BODY,{"disambiguationData":[OSD([sQuery(id+"F0.wireOp",EDGE,"E1")])]}),"instanceName":"1"}),"instanceName":"1"}),"instanceName":"1"}),"instanceName":"1"}),"instanceName":"1"}),"instanceName":"1"});
            var Q179;
            Q179=makeQuery(id+"F9.opPattern","COPY",BODY,{"derivedFrom":makeQuery(id+"F8.opPattern","COPY",BODY,{"derivedFrom":makeQuery(id+"F7.opPattern","COPY",BODY,{"derivedFrom":makeQuery(id+"F5.opPattern","COPY",BODY,{"derivedFrom":makeQuery(id+"F4.opPattern","COPY",BODY,{"derivedFrom":makeQuery(id+"F3.opPattern","COPY",BODY,{"derivedFrom":makeQuery(id+"F2.opPattern","COPY",BODY,{"derivedFrom":makeQuery(id+"F1.opRevolve","SWEPT_BODY",BODY,{"disambiguationData":[OSD([sQuery(id+"F0.wireOp",EDGE,"E1")])]}),"instanceName":"1"}),"instanceName":"1"}),"instanceName":"1"}),"instanceName":"1"}),"instanceName":"1"}),"instanceName":"1"}),"instanceName":"1"});
            var Q180;
            Q180=makeQuery(id+"F9.opPattern","COPY",BODY,{"derivedFrom":makeQuery(id+"F8.opPattern","COPY",BODY,{"derivedFrom":makeQuery(id+"F7.opPattern","COPY",BODY,{"derivedFrom":makeQuery(id+"F6.opPattern","COPY",BODY,{"derivedFrom":makeQuery(id+"F1.opRevolve","SWEPT_BODY",BODY,{"disambiguationData":[OSD([sQuery(id+"F0.wireOp",EDGE,"E1")])]}),"instanceName":"1"}),"instanceName":"1"}),"instanceName":"1"}),"instanceName":"1"});
            var Q181;
            Q181=makeQuery(id+"F9.opPattern","COPY",BODY,{"derivedFrom":makeQuery(id+"F8.opPattern","COPY",BODY,{"derivedFrom":makeQuery(id+"F7.opPattern","COPY",BODY,{"derivedFrom":makeQuery(id+"F6.opPattern","COPY",BODY,{"derivedFrom":makeQuery(id+"F2.opPattern","COPY",BODY,{"derivedFrom":makeQuery(id+"F1.opRevolve","SWEPT_BODY",BODY,{"disambiguationData":[OSD([sQuery(id+"F0.wireOp",EDGE,"E1")])]}),"instanceName":"1"}),"instanceName":"1"}),"instanceName":"1"}),"instanceName":"1"}),"instanceName":"1"});
            var Q182;
            Q182=makeQuery(id+"F9.opPattern","COPY",BODY,{"derivedFrom":makeQuery(id+"F8.opPattern","COPY",BODY,{"derivedFrom":makeQuery(id+"F7.opPattern","COPY",BODY,{"derivedFrom":makeQuery(id+"F6.opPattern","COPY",BODY,{"derivedFrom":makeQuery(id+"F3.opPattern","COPY",BODY,{"derivedFrom":makeQuery(id+"F2.opPattern","COPY",BODY,{"derivedFrom":makeQuery(id+"F1.opRevolve","SWEPT_BODY",BODY,{"disambiguationData":[OSD([sQuery(id+"F0.wireOp",EDGE,"E1")])]}),"instanceName":"1"}),"instanceName":"1"}),"instanceName":"1"}),"instanceName":"1"}),"instanceName":"1"}),"instanceName":"1"});
            var Q183;
            Q183=makeQuery(id+"F9.opPattern","COPY",BODY,{"derivedFrom":makeQuery(id+"F8.opPattern","COPY",BODY,{"derivedFrom":makeQuery(id+"F7.opPattern","COPY",BODY,{"derivedFrom":makeQuery(id+"F6.opPattern","COPY",BODY,{"derivedFrom":makeQuery(id+"F4.opPattern","COPY",BODY,{"derivedFrom":makeQuery(id+"F1.opRevolve","SWEPT_BODY",BODY,{"disambiguationData":[OSD([sQuery(id+"F0.wireOp",EDGE,"E1")])]}),"instanceName":"1"}),"instanceName":"1"}),"instanceName":"1"}),"instanceName":"1"}),"instanceName":"1"});
            var Q184;
            Q184=makeQuery(id+"F9.opPattern","COPY",BODY,{"derivedFrom":makeQuery(id+"F8.opPattern","COPY",BODY,{"derivedFrom":makeQuery(id+"F7.opPattern","COPY",BODY,{"derivedFrom":makeQuery(id+"F6.opPattern","COPY",BODY,{"derivedFrom":makeQuery(id+"F4.opPattern","COPY",BODY,{"derivedFrom":makeQuery(id+"F2.opPattern","COPY",BODY,{"derivedFrom":makeQuery(id+"F1.opRevolve","SWEPT_BODY",BODY,{"disambiguationData":[OSD([sQuery(id+"F0.wireOp",EDGE,"E1")])]}),"instanceName":"1"}),"instanceName":"1"}),"instanceName":"1"}),"instanceName":"1"}),"instanceName":"1"}),"instanceName":"1"});
            var Q185;
            Q185=makeQuery(id+"F9.opPattern","COPY",BODY,{"derivedFrom":makeQuery(id+"F8.opPattern","COPY",BODY,{"derivedFrom":makeQuery(id+"F7.opPattern","COPY",BODY,{"derivedFrom":makeQuery(id+"F6.opPattern","COPY",BODY,{"derivedFrom":makeQuery(id+"F4.opPattern","COPY",BODY,{"derivedFrom":makeQuery(id+"F3.opPattern","COPY",BODY,{"derivedFrom":makeQuery(id+"F2.opPattern","COPY",BODY,{"derivedFrom":makeQuery(id+"F1.opRevolve","SWEPT_BODY",BODY,{"disambiguationData":[OSD([sQuery(id+"F0.wireOp",EDGE,"E1")])]}),"instanceName":"1"}),"instanceName":"1"}),"instanceName":"1"}),"instanceName":"1"}),"instanceName":"1"}),"instanceName":"1"}),"instanceName":"1"});
            var Q186;
            Q186=makeQuery(id+"F9.opPattern","COPY",BODY,{"derivedFrom":makeQuery(id+"F8.opPattern","COPY",BODY,{"derivedFrom":makeQuery(id+"F7.opPattern","COPY",BODY,{"derivedFrom":makeQuery(id+"F6.opPattern","COPY",BODY,{"derivedFrom":makeQuery(id+"F5.opPattern","COPY",BODY,{"derivedFrom":makeQuery(id+"F1.opRevolve","SWEPT_BODY",BODY,{"disambiguationData":[OSD([sQuery(id+"F0.wireOp",EDGE,"E1")])]}),"instanceName":"1"}),"instanceName":"1"}),"instanceName":"1"}),"instanceName":"1"}),"instanceName":"1"});
            var Q187;
            Q187=makeQuery(id+"F9.opPattern","COPY",BODY,{"derivedFrom":makeQuery(id+"F8.opPattern","COPY",BODY,{"derivedFrom":makeQuery(id+"F7.opPattern","COPY",BODY,{"derivedFrom":makeQuery(id+"F6.opPattern","COPY",BODY,{"derivedFrom":makeQuery(id+"F5.opPattern","COPY",BODY,{"derivedFrom":makeQuery(id+"F2.opPattern","COPY",BODY,{"derivedFrom":makeQuery(id+"F1.opRevolve","SWEPT_BODY",BODY,{"disambiguationData":[OSD([sQuery(id+"F0.wireOp",EDGE,"E1")])]}),"instanceName":"1"}),"instanceName":"1"}),"instanceName":"1"}),"instanceName":"1"}),"instanceName":"1"}),"instanceName":"1"});
            var Q188;
            Q188=makeQuery(id+"F9.opPattern","COPY",BODY,{"derivedFrom":makeQuery(id+"F8.opPattern","COPY",BODY,{"derivedFrom":makeQuery(id+"F7.opPattern","COPY",BODY,{"derivedFrom":makeQuery(id+"F6.opPattern","COPY",BODY,{"derivedFrom":makeQuery(id+"F5.opPattern","COPY",BODY,{"derivedFrom":makeQuery(id+"F3.opPattern","COPY",BODY,{"derivedFrom":makeQuery(id+"F2.opPattern","COPY",BODY,{"derivedFrom":makeQuery(id+"F1.opRevolve","SWEPT_BODY",BODY,{"disambiguationData":[OSD([sQuery(id+"F0.wireOp",EDGE,"E1")])]}),"instanceName":"1"}),"instanceName":"1"}),"instanceName":"1"}),"instanceName":"1"}),"instanceName":"1"}),"instanceName":"1"}),"instanceName":"1"});
            var Q189;
            Q189=makeQuery(id+"F9.opPattern","COPY",BODY,{"derivedFrom":makeQuery(id+"F8.opPattern","COPY",BODY,{"derivedFrom":makeQuery(id+"F7.opPattern","COPY",BODY,{"derivedFrom":makeQuery(id+"F6.opPattern","COPY",BODY,{"derivedFrom":makeQuery(id+"F5.opPattern","COPY",BODY,{"derivedFrom":makeQuery(id+"F4.opPattern","COPY",BODY,{"derivedFrom":makeQuery(id+"F1.opRevolve","SWEPT_BODY",BODY,{"disambiguationData":[OSD([sQuery(id+"F0.wireOp",EDGE,"E1")])]}),"instanceName":"1"}),"instanceName":"1"}),"instanceName":"1"}),"instanceName":"1"}),"instanceName":"1"}),"instanceName":"1"});
            var Q190;
            Q190=makeQuery(id+"F9.opPattern","COPY",BODY,{"derivedFrom":makeQuery(id+"F8.opPattern","COPY",BODY,{"derivedFrom":makeQuery(id+"F7.opPattern","COPY",BODY,{"derivedFrom":makeQuery(id+"F6.opPattern","COPY",BODY,{"derivedFrom":makeQuery(id+"F5.opPattern","COPY",BODY,{"derivedFrom":makeQuery(id+"F4.opPattern","COPY",BODY,{"derivedFrom":makeQuery(id+"F2.opPattern","COPY",BODY,{"derivedFrom":makeQuery(id+"F1.opRevolve","SWEPT_BODY",BODY,{"disambiguationData":[OSD([sQuery(id+"F0.wireOp",EDGE,"E1")])]}),"instanceName":"1"}),"instanceName":"1"}),"instanceName":"1"}),"instanceName":"1"}),"instanceName":"1"}),"instanceName":"1"}),"instanceName":"1"});
            var Q191;
            Q191=makeQuery(id+"F9.opPattern","COPY",BODY,{"derivedFrom":makeQuery(id+"F8.opPattern","COPY",BODY,{"derivedFrom":makeQuery(id+"F7.opPattern","COPY",BODY,{"derivedFrom":makeQuery(id+"F6.opPattern","COPY",BODY,{"derivedFrom":makeQuery(id+"F5.opPattern","COPY",BODY,{"derivedFrom":makeQuery(id+"F4.opPattern","COPY",BODY,{"derivedFrom":makeQuery(id+"F3.opPattern","COPY",BODY,{"derivedFrom":makeQuery(id+"F2.opPattern","COPY",BODY,{"derivedFrom":makeQuery(id+"F1.opRevolve","SWEPT_BODY",BODY,{"disambiguationData":[OSD([sQuery(id+"F0.wireOp",EDGE,"E1")])]}),"instanceName":"1"}),"instanceName":"1"}),"instanceName":"1"}),"instanceName":"1"}),"instanceName":"1"}),"instanceName":"1"}),"instanceName":"1"}),"instanceName":"1"});
            transform(context, id + "F10", {"entities" : qUnion([Q0, Q1, Q2, Q3, Q4, Q5, Q6, Q7, Q8, Q9, Q10, Q11, Q12, Q13, Q14, Q15, Q16, Q17, Q18, Q19, Q20, Q21, Q22, Q23, Q24, Q25, Q26, Q27, Q28, Q29, Q30, Q31, Q32, Q33, Q34, Q35, Q36, Q37, Q38, Q39, Q40, Q41, Q42, Q43, Q44, Q45, Q46, Q47, Q48, Q49, Q50, Q51, Q52, Q53, Q54, Q55, Q56, Q57, Q58, Q59, Q60, Q61, Q62, Q63, Q64, Q65, Q66, Q67, Q68, Q69, Q70, Q71, Q72, Q73, Q74, Q75, Q76, Q77, Q78, Q79, Q80, Q81, Q82, Q83, Q84, Q85, Q86, Q87, Q88, Q89, Q90, Q91, Q92, Q93, Q94, Q95, Q96, Q97, Q98, Q99, Q100, Q101, Q102, Q103, Q104, Q105, Q106, Q107, Q108, Q109, Q110, Q111, Q112, Q113, Q114, Q115, Q116, Q117, Q118, Q119, Q120, Q121, Q122, Q123, Q124, Q125, Q126, Q127, Q128, Q129, Q130, Q131, Q132, Q133, Q134, Q135, Q136, Q137, Q138, Q139, Q140, Q141, Q142, Q143, Q144, Q145, Q146, Q147, Q148, Q149, Q150, Q151, Q152, Q153, Q154, Q155, Q156, Q157, Q158, Q159, Q160, Q161, Q162, Q163, Q164, Q165, Q166, Q167, Q168, Q169, Q170, Q171, Q172, Q173, Q174, Q175, Q176, Q177, Q178, Q179, Q180, Q181, Q182, Q183, Q184, Q185, Q186, Q187, Q188, Q189, Q190, Q191]), "transformType" : TransformType.TRANSLATION_3D, "dx" : 0 * mm, "dy" : 0.14 * mm, "dz" : 0 * mm, "makeCopy" : true});
        }
        {
            var Q0;
            Q0=makeQuery(id+"F1.opRevolve","SWEPT_BODY",BODY,{"disambiguationData":[OSD([sQuery(id+"F0.wireOp",EDGE,"E1")])]});
            var Q1;
            Q1=makeQuery(id+"F2.opPattern","COPY",BODY,{"derivedFrom":makeQuery(id+"F1.opRevolve","SWEPT_BODY",BODY,{"disambiguationData":[OSD([sQuery(id+"F0.wireOp",EDGE,"E1")])]}),"instanceName":"1"});
            var Q2;
            Q2=makeQuery(id+"F3.opPattern","COPY",BODY,{"derivedFrom":makeQuery(id+"F2.opPattern","COPY",BODY,{"derivedFrom":makeQuery(id+"F1.opRevolve","SWEPT_BODY",BODY,{"disambiguationData":[OSD([sQuery(id+"F0.wireOp",EDGE,"E1")])]}),"instanceName":"1"}),"instanceName":"1"});
            var Q3;
            Q3=makeQuery(id+"F4.opPattern","COPY",BODY,{"derivedFrom":makeQuery(id+"F1.opRevolve","SWEPT_BODY",BODY,{"disambiguationData":[OSD([sQuery(id+"F0.wireOp",EDGE,"E1")])]}),"instanceName":"1"});
            var Q4;
            Q4=makeQuery(id+"F4.opPattern","COPY",BODY,{"derivedFrom":makeQuery(id+"F2.opPattern","COPY",BODY,{"derivedFrom":makeQuery(id+"F1.opRevolve","SWEPT_BODY",BODY,{"disambiguationData":[OSD([sQuery(id+"F0.wireOp",EDGE,"E1")])]}),"instanceName":"1"}),"instanceName":"1"});
            var Q5;
            Q5=makeQuery(id+"F4.opPattern","COPY",BODY,{"derivedFrom":makeQuery(id+"F3.opPattern","COPY",BODY,{"derivedFrom":makeQuery(id+"F2.opPattern","COPY",BODY,{"derivedFrom":makeQuery(id+"F1.opRevolve","SWEPT_BODY",BODY,{"disambiguationData":[OSD([sQuery(id+"F0.wireOp",EDGE,"E1")])]}),"instanceName":"1"}),"instanceName":"1"}),"instanceName":"1"});
            var Q6;
            Q6=makeQuery(id+"F5.opPattern","COPY",BODY,{"derivedFrom":makeQuery(id+"F1.opRevolve","SWEPT_BODY",BODY,{"disambiguationData":[OSD([sQuery(id+"F0.wireOp",EDGE,"E1")])]}),"instanceName":"1"});
            var Q7;
            Q7=makeQuery(id+"F5.opPattern","COPY",BODY,{"derivedFrom":makeQuery(id+"F2.opPattern","COPY",BODY,{"derivedFrom":makeQuery(id+"F1.opRevolve","SWEPT_BODY",BODY,{"disambiguationData":[OSD([sQuery(id+"F0.wireOp",EDGE,"E1")])]}),"instanceName":"1"}),"instanceName":"1"});
            var Q8;
            Q8=makeQuery(id+"F5.opPattern","COPY",BODY,{"derivedFrom":makeQuery(id+"F3.opPattern","COPY",BODY,{"derivedFrom":makeQuery(id+"F2.opPattern","COPY",BODY,{"derivedFrom":makeQuery(id+"F1.opRevolve","SWEPT_BODY",BODY,{"disambiguationData":[OSD([sQuery(id+"F0.wireOp",EDGE,"E1")])]}),"instanceName":"1"}),"instanceName":"1"}),"instanceName":"1"});
            var Q9;
            Q9=makeQuery(id+"F5.opPattern","COPY",BODY,{"derivedFrom":makeQuery(id+"F4.opPattern","COPY",BODY,{"derivedFrom":makeQuery(id+"F1.opRevolve","SWEPT_BODY",BODY,{"disambiguationData":[OSD([sQuery(id+"F0.wireOp",EDGE,"E1")])]}),"instanceName":"1"}),"instanceName":"1"});
            var Q10;
            Q10=makeQuery(id+"F5.opPattern","COPY",BODY,{"derivedFrom":makeQuery(id+"F4.opPattern","COPY",BODY,{"derivedFrom":makeQuery(id+"F2.opPattern","COPY",BODY,{"derivedFrom":makeQuery(id+"F1.opRevolve","SWEPT_BODY",BODY,{"disambiguationData":[OSD([sQuery(id+"F0.wireOp",EDGE,"E1")])]}),"instanceName":"1"}),"instanceName":"1"}),"instanceName":"1"});
            var Q11;
            Q11=makeQuery(id+"F5.opPattern","COPY",BODY,{"derivedFrom":makeQuery(id+"F4.opPattern","COPY",BODY,{"derivedFrom":makeQuery(id+"F3.opPattern","COPY",BODY,{"derivedFrom":makeQuery(id+"F2.opPattern","COPY",BODY,{"derivedFrom":makeQuery(id+"F1.opRevolve","SWEPT_BODY",BODY,{"disambiguationData":[OSD([sQuery(id+"F0.wireOp",EDGE,"E1")])]}),"instanceName":"1"}),"instanceName":"1"}),"instanceName":"1"}),"instanceName":"1"});
            var Q12;
            Q12=makeQuery(id+"F6.opPattern","COPY",BODY,{"derivedFrom":makeQuery(id+"F1.opRevolve","SWEPT_BODY",BODY,{"disambiguationData":[OSD([sQuery(id+"F0.wireOp",EDGE,"E1")])]}),"instanceName":"1"});
            var Q13;
            Q13=makeQuery(id+"F6.opPattern","COPY",BODY,{"derivedFrom":makeQuery(id+"F2.opPattern","COPY",BODY,{"derivedFrom":makeQuery(id+"F1.opRevolve","SWEPT_BODY",BODY,{"disambiguationData":[OSD([sQuery(id+"F0.wireOp",EDGE,"E1")])]}),"instanceName":"1"}),"instanceName":"1"});
            var Q14;
            Q14=makeQuery(id+"F6.opPattern","COPY",BODY,{"derivedFrom":makeQuery(id+"F3.opPattern","COPY",BODY,{"derivedFrom":makeQuery(id+"F2.opPattern","COPY",BODY,{"derivedFrom":makeQuery(id+"F1.opRevolve","SWEPT_BODY",BODY,{"disambiguationData":[OSD([sQuery(id+"F0.wireOp",EDGE,"E1")])]}),"instanceName":"1"}),"instanceName":"1"}),"instanceName":"1"});
            var Q15;
            Q15=makeQuery(id+"F6.opPattern","COPY",BODY,{"derivedFrom":makeQuery(id+"F4.opPattern","COPY",BODY,{"derivedFrom":makeQuery(id+"F1.opRevolve","SWEPT_BODY",BODY,{"disambiguationData":[OSD([sQuery(id+"F0.wireOp",EDGE,"E1")])]}),"instanceName":"1"}),"instanceName":"1"});
            var Q16;
            Q16=makeQuery(id+"F6.opPattern","COPY",BODY,{"derivedFrom":makeQuery(id+"F4.opPattern","COPY",BODY,{"derivedFrom":makeQuery(id+"F2.opPattern","COPY",BODY,{"derivedFrom":makeQuery(id+"F1.opRevolve","SWEPT_BODY",BODY,{"disambiguationData":[OSD([sQuery(id+"F0.wireOp",EDGE,"E1")])]}),"instanceName":"1"}),"instanceName":"1"}),"instanceName":"1"});
            var Q17;
            Q17=makeQuery(id+"F6.opPattern","COPY",BODY,{"derivedFrom":makeQuery(id+"F4.opPattern","COPY",BODY,{"derivedFrom":makeQuery(id+"F3.opPattern","COPY",BODY,{"derivedFrom":makeQuery(id+"F2.opPattern","COPY",BODY,{"derivedFrom":makeQuery(id+"F1.opRevolve","SWEPT_BODY",BODY,{"disambiguationData":[OSD([sQuery(id+"F0.wireOp",EDGE,"E1")])]}),"instanceName":"1"}),"instanceName":"1"}),"instanceName":"1"}),"instanceName":"1"});
            var Q18;
            Q18=makeQuery(id+"F6.opPattern","COPY",BODY,{"derivedFrom":makeQuery(id+"F5.opPattern","COPY",BODY,{"derivedFrom":makeQuery(id+"F1.opRevolve","SWEPT_BODY",BODY,{"disambiguationData":[OSD([sQuery(id+"F0.wireOp",EDGE,"E1")])]}),"instanceName":"1"}),"instanceName":"1"});
            var Q19;
            Q19=makeQuery(id+"F6.opPattern","COPY",BODY,{"derivedFrom":makeQuery(id+"F5.opPattern","COPY",BODY,{"derivedFrom":makeQuery(id+"F2.opPattern","COPY",BODY,{"derivedFrom":makeQuery(id+"F1.opRevolve","SWEPT_BODY",BODY,{"disambiguationData":[OSD([sQuery(id+"F0.wireOp",EDGE,"E1")])]}),"instanceName":"1"}),"instanceName":"1"}),"instanceName":"1"});
            var Q20;
            Q20=makeQuery(id+"F6.opPattern","COPY",BODY,{"derivedFrom":makeQuery(id+"F5.opPattern","COPY",BODY,{"derivedFrom":makeQuery(id+"F3.opPattern","COPY",BODY,{"derivedFrom":makeQuery(id+"F2.opPattern","COPY",BODY,{"derivedFrom":makeQuery(id+"F1.opRevolve","SWEPT_BODY",BODY,{"disambiguationData":[OSD([sQuery(id+"F0.wireOp",EDGE,"E1")])]}),"instanceName":"1"}),"instanceName":"1"}),"instanceName":"1"}),"instanceName":"1"});
            var Q21;
            Q21=makeQuery(id+"F6.opPattern","COPY",BODY,{"derivedFrom":makeQuery(id+"F5.opPattern","COPY",BODY,{"derivedFrom":makeQuery(id+"F4.opPattern","COPY",BODY,{"derivedFrom":makeQuery(id+"F1.opRevolve","SWEPT_BODY",BODY,{"disambiguationData":[OSD([sQuery(id+"F0.wireOp",EDGE,"E1")])]}),"instanceName":"1"}),"instanceName":"1"}),"instanceName":"1"});
            var Q22;
            Q22=makeQuery(id+"F6.opPattern","COPY",BODY,{"derivedFrom":makeQuery(id+"F5.opPattern","COPY",BODY,{"derivedFrom":makeQuery(id+"F4.opPattern","COPY",BODY,{"derivedFrom":makeQuery(id+"F2.opPattern","COPY",BODY,{"derivedFrom":makeQuery(id+"F1.opRevolve","SWEPT_BODY",BODY,{"disambiguationData":[OSD([sQuery(id+"F0.wireOp",EDGE,"E1")])]}),"instanceName":"1"}),"instanceName":"1"}),"instanceName":"1"}),"instanceName":"1"});
            var Q23;
            Q23=makeQuery(id+"F6.opPattern","COPY",BODY,{"derivedFrom":makeQuery(id+"F5.opPattern","COPY",BODY,{"derivedFrom":makeQuery(id+"F4.opPattern","COPY",BODY,{"derivedFrom":makeQuery(id+"F3.opPattern","COPY",BODY,{"derivedFrom":makeQuery(id+"F2.opPattern","COPY",BODY,{"derivedFrom":makeQuery(id+"F1.opRevolve","SWEPT_BODY",BODY,{"disambiguationData":[OSD([sQuery(id+"F0.wireOp",EDGE,"E1")])]}),"instanceName":"1"}),"instanceName":"1"}),"instanceName":"1"}),"instanceName":"1"}),"instanceName":"1"});
            var Q24;
            Q24=makeQuery(id+"F7.opPattern","COPY",BODY,{"derivedFrom":makeQuery(id+"F1.opRevolve","SWEPT_BODY",BODY,{"disambiguationData":[OSD([sQuery(id+"F0.wireOp",EDGE,"E1")])]}),"instanceName":"1"});
            var Q25;
            Q25=makeQuery(id+"F7.opPattern","COPY",BODY,{"derivedFrom":makeQuery(id+"F2.opPattern","COPY",BODY,{"derivedFrom":makeQuery(id+"F1.opRevolve","SWEPT_BODY",BODY,{"disambiguationData":[OSD([sQuery(id+"F0.wireOp",EDGE,"E1")])]}),"instanceName":"1"}),"instanceName":"1"});
            var Q26;
            Q26=makeQuery(id+"F7.opPattern","COPY",BODY,{"derivedFrom":makeQuery(id+"F3.opPattern","COPY",BODY,{"derivedFrom":makeQuery(id+"F2.opPattern","COPY",BODY,{"derivedFrom":makeQuery(id+"F1.opRevolve","SWEPT_BODY",BODY,{"disambiguationData":[OSD([sQuery(id+"F0.wireOp",EDGE,"E1")])]}),"instanceName":"1"}),"instanceName":"1"}),"instanceName":"1"});
            var Q27;
            Q27=makeQuery(id+"F7.opPattern","COPY",BODY,{"derivedFrom":makeQuery(id+"F4.opPattern","COPY",BODY,{"derivedFrom":makeQuery(id+"F1.opRevolve","SWEPT_BODY",BODY,{"disambiguationData":[OSD([sQuery(id+"F0.wireOp",EDGE,"E1")])]}),"instanceName":"1"}),"instanceName":"1"});
            var Q28;
            Q28=makeQuery(id+"F7.opPattern","COPY",BODY,{"derivedFrom":makeQuery(id+"F4.opPattern","COPY",BODY,{"derivedFrom":makeQuery(id+"F2.opPattern","COPY",BODY,{"derivedFrom":makeQuery(id+"F1.opRevolve","SWEPT_BODY",BODY,{"disambiguationData":[OSD([sQuery(id+"F0.wireOp",EDGE,"E1")])]}),"instanceName":"1"}),"instanceName":"1"}),"instanceName":"1"});
            var Q29;
            Q29=makeQuery(id+"F7.opPattern","COPY",BODY,{"derivedFrom":makeQuery(id+"F4.opPattern","COPY",BODY,{"derivedFrom":makeQuery(id+"F3.opPattern","COPY",BODY,{"derivedFrom":makeQuery(id+"F2.opPattern","COPY",BODY,{"derivedFrom":makeQuery(id+"F1.opRevolve","SWEPT_BODY",BODY,{"disambiguationData":[OSD([sQuery(id+"F0.wireOp",EDGE,"E1")])]}),"instanceName":"1"}),"instanceName":"1"}),"instanceName":"1"}),"instanceName":"1"});
            var Q30;
            Q30=makeQuery(id+"F7.opPattern","COPY",BODY,{"derivedFrom":makeQuery(id+"F5.opPattern","COPY",BODY,{"derivedFrom":makeQuery(id+"F1.opRevolve","SWEPT_BODY",BODY,{"disambiguationData":[OSD([sQuery(id+"F0.wireOp",EDGE,"E1")])]}),"instanceName":"1"}),"instanceName":"1"});
            var Q31;
            Q31=makeQuery(id+"F7.opPattern","COPY",BODY,{"derivedFrom":makeQuery(id+"F5.opPattern","COPY",BODY,{"derivedFrom":makeQuery(id+"F2.opPattern","COPY",BODY,{"derivedFrom":makeQuery(id+"F1.opRevolve","SWEPT_BODY",BODY,{"disambiguationData":[OSD([sQuery(id+"F0.wireOp",EDGE,"E1")])]}),"instanceName":"1"}),"instanceName":"1"}),"instanceName":"1"});
            var Q32;
            Q32=makeQuery(id+"F7.opPattern","COPY",BODY,{"derivedFrom":makeQuery(id+"F5.opPattern","COPY",BODY,{"derivedFrom":makeQuery(id+"F3.opPattern","COPY",BODY,{"derivedFrom":makeQuery(id+"F2.opPattern","COPY",BODY,{"derivedFrom":makeQuery(id+"F1.opRevolve","SWEPT_BODY",BODY,{"disambiguationData":[OSD([sQuery(id+"F0.wireOp",EDGE,"E1")])]}),"instanceName":"1"}),"instanceName":"1"}),"instanceName":"1"}),"instanceName":"1"});
            var Q33;
            Q33=makeQuery(id+"F7.opPattern","COPY",BODY,{"derivedFrom":makeQuery(id+"F5.opPattern","COPY",BODY,{"derivedFrom":makeQuery(id+"F4.opPattern","COPY",BODY,{"derivedFrom":makeQuery(id+"F1.opRevolve","SWEPT_BODY",BODY,{"disambiguationData":[OSD([sQuery(id+"F0.wireOp",EDGE,"E1")])]}),"instanceName":"1"}),"instanceName":"1"}),"instanceName":"1"});
            var Q34;
            Q34=makeQuery(id+"F7.opPattern","COPY",BODY,{"derivedFrom":makeQuery(id+"F5.opPattern","COPY",BODY,{"derivedFrom":makeQuery(id+"F4.opPattern","COPY",BODY,{"derivedFrom":makeQuery(id+"F2.opPattern","COPY",BODY,{"derivedFrom":makeQuery(id+"F1.opRevolve","SWEPT_BODY",BODY,{"disambiguationData":[OSD([sQuery(id+"F0.wireOp",EDGE,"E1")])]}),"instanceName":"1"}),"instanceName":"1"}),"instanceName":"1"}),"instanceName":"1"});
            var Q35;
            Q35=makeQuery(id+"F7.opPattern","COPY",BODY,{"derivedFrom":makeQuery(id+"F5.opPattern","COPY",BODY,{"derivedFrom":makeQuery(id+"F4.opPattern","COPY",BODY,{"derivedFrom":makeQuery(id+"F3.opPattern","COPY",BODY,{"derivedFrom":makeQuery(id+"F2.opPattern","COPY",BODY,{"derivedFrom":makeQuery(id+"F1.opRevolve","SWEPT_BODY",BODY,{"disambiguationData":[OSD([sQuery(id+"F0.wireOp",EDGE,"E1")])]}),"instanceName":"1"}),"instanceName":"1"}),"instanceName":"1"}),"instanceName":"1"}),"instanceName":"1"});
            var Q36;
            Q36=makeQuery(id+"F7.opPattern","COPY",BODY,{"derivedFrom":makeQuery(id+"F6.opPattern","COPY",BODY,{"derivedFrom":makeQuery(id+"F1.opRevolve","SWEPT_BODY",BODY,{"disambiguationData":[OSD([sQuery(id+"F0.wireOp",EDGE,"E1")])]}),"instanceName":"1"}),"instanceName":"1"});
            var Q37;
            Q37=makeQuery(id+"F7.opPattern","COPY",BODY,{"derivedFrom":makeQuery(id+"F6.opPattern","COPY",BODY,{"derivedFrom":makeQuery(id+"F2.opPattern","COPY",BODY,{"derivedFrom":makeQuery(id+"F1.opRevolve","SWEPT_BODY",BODY,{"disambiguationData":[OSD([sQuery(id+"F0.wireOp",EDGE,"E1")])]}),"instanceName":"1"}),"instanceName":"1"}),"instanceName":"1"});
            var Q38;
            Q38=makeQuery(id+"F7.opPattern","COPY",BODY,{"derivedFrom":makeQuery(id+"F6.opPattern","COPY",BODY,{"derivedFrom":makeQuery(id+"F3.opPattern","COPY",BODY,{"derivedFrom":makeQuery(id+"F2.opPattern","COPY",BODY,{"derivedFrom":makeQuery(id+"F1.opRevolve","SWEPT_BODY",BODY,{"disambiguationData":[OSD([sQuery(id+"F0.wireOp",EDGE,"E1")])]}),"instanceName":"1"}),"instanceName":"1"}),"instanceName":"1"}),"instanceName":"1"});
            var Q39;
            Q39=makeQuery(id+"F7.opPattern","COPY",BODY,{"derivedFrom":makeQuery(id+"F6.opPattern","COPY",BODY,{"derivedFrom":makeQuery(id+"F4.opPattern","COPY",BODY,{"derivedFrom":makeQuery(id+"F1.opRevolve","SWEPT_BODY",BODY,{"disambiguationData":[OSD([sQuery(id+"F0.wireOp",EDGE,"E1")])]}),"instanceName":"1"}),"instanceName":"1"}),"instanceName":"1"});
            var Q40;
            Q40=makeQuery(id+"F7.opPattern","COPY",BODY,{"derivedFrom":makeQuery(id+"F6.opPattern","COPY",BODY,{"derivedFrom":makeQuery(id+"F4.opPattern","COPY",BODY,{"derivedFrom":makeQuery(id+"F2.opPattern","COPY",BODY,{"derivedFrom":makeQuery(id+"F1.opRevolve","SWEPT_BODY",BODY,{"disambiguationData":[OSD([sQuery(id+"F0.wireOp",EDGE,"E1")])]}),"instanceName":"1"}),"instanceName":"1"}),"instanceName":"1"}),"instanceName":"1"});
            var Q41;
            Q41=makeQuery(id+"F7.opPattern","COPY",BODY,{"derivedFrom":makeQuery(id+"F6.opPattern","COPY",BODY,{"derivedFrom":makeQuery(id+"F4.opPattern","COPY",BODY,{"derivedFrom":makeQuery(id+"F3.opPattern","COPY",BODY,{"derivedFrom":makeQuery(id+"F2.opPattern","COPY",BODY,{"derivedFrom":makeQuery(id+"F1.opRevolve","SWEPT_BODY",BODY,{"disambiguationData":[OSD([sQuery(id+"F0.wireOp",EDGE,"E1")])]}),"instanceName":"1"}),"instanceName":"1"}),"instanceName":"1"}),"instanceName":"1"}),"instanceName":"1"});
            var Q42;
            Q42=makeQuery(id+"F7.opPattern","COPY",BODY,{"derivedFrom":makeQuery(id+"F6.opPattern","COPY",BODY,{"derivedFrom":makeQuery(id+"F5.opPattern","COPY",BODY,{"derivedFrom":makeQuery(id+"F1.opRevolve","SWEPT_BODY",BODY,{"disambiguationData":[OSD([sQuery(id+"F0.wireOp",EDGE,"E1")])]}),"instanceName":"1"}),"instanceName":"1"}),"instanceName":"1"});
            var Q43;
            Q43=makeQuery(id+"F7.opPattern","COPY",BODY,{"derivedFrom":makeQuery(id+"F6.opPattern","COPY",BODY,{"derivedFrom":makeQuery(id+"F5.opPattern","COPY",BODY,{"derivedFrom":makeQuery(id+"F2.opPattern","COPY",BODY,{"derivedFrom":makeQuery(id+"F1.opRevolve","SWEPT_BODY",BODY,{"disambiguationData":[OSD([sQuery(id+"F0.wireOp",EDGE,"E1")])]}),"instanceName":"1"}),"instanceName":"1"}),"instanceName":"1"}),"instanceName":"1"});
            var Q44;
            Q44=makeQuery(id+"F7.opPattern","COPY",BODY,{"derivedFrom":makeQuery(id+"F6.opPattern","COPY",BODY,{"derivedFrom":makeQuery(id+"F5.opPattern","COPY",BODY,{"derivedFrom":makeQuery(id+"F3.opPattern","COPY",BODY,{"derivedFrom":makeQuery(id+"F2.opPattern","COPY",BODY,{"derivedFrom":makeQuery(id+"F1.opRevolve","SWEPT_BODY",BODY,{"disambiguationData":[OSD([sQuery(id+"F0.wireOp",EDGE,"E1")])]}),"instanceName":"1"}),"instanceName":"1"}),"instanceName":"1"}),"instanceName":"1"}),"instanceName":"1"});
            var Q45;
            Q45=makeQuery(id+"F7.opPattern","COPY",BODY,{"derivedFrom":makeQuery(id+"F6.opPattern","COPY",BODY,{"derivedFrom":makeQuery(id+"F5.opPattern","COPY",BODY,{"derivedFrom":makeQuery(id+"F4.opPattern","COPY",BODY,{"derivedFrom":makeQuery(id+"F1.opRevolve","SWEPT_BODY",BODY,{"disambiguationData":[OSD([sQuery(id+"F0.wireOp",EDGE,"E1")])]}),"instanceName":"1"}),"instanceName":"1"}),"instanceName":"1"}),"instanceName":"1"});
            var Q46;
            Q46=makeQuery(id+"F7.opPattern","COPY",BODY,{"derivedFrom":makeQuery(id+"F6.opPattern","COPY",BODY,{"derivedFrom":makeQuery(id+"F5.opPattern","COPY",BODY,{"derivedFrom":makeQuery(id+"F4.opPattern","COPY",BODY,{"derivedFrom":makeQuery(id+"F2.opPattern","COPY",BODY,{"derivedFrom":makeQuery(id+"F1.opRevolve","SWEPT_BODY",BODY,{"disambiguationData":[OSD([sQuery(id+"F0.wireOp",EDGE,"E1")])]}),"instanceName":"1"}),"instanceName":"1"}),"instanceName":"1"}),"instanceName":"1"}),"instanceName":"1"});
            var Q47;
            Q47=makeQuery(id+"F7.opPattern","COPY",BODY,{"derivedFrom":makeQuery(id+"F6.opPattern","COPY",BODY,{"derivedFrom":makeQuery(id+"F5.opPattern","COPY",BODY,{"derivedFrom":makeQuery(id+"F4.opPattern","COPY",BODY,{"derivedFrom":makeQuery(id+"F3.opPattern","COPY",BODY,{"derivedFrom":makeQuery(id+"F2.opPattern","COPY",BODY,{"derivedFrom":makeQuery(id+"F1.opRevolve","SWEPT_BODY",BODY,{"disambiguationData":[OSD([sQuery(id+"F0.wireOp",EDGE,"E1")])]}),"instanceName":"1"}),"instanceName":"1"}),"instanceName":"1"}),"instanceName":"1"}),"instanceName":"1"}),"instanceName":"1"});
            var Q48;
            Q48=makeQuery(id+"F8.opPattern","COPY",BODY,{"derivedFrom":makeQuery(id+"F1.opRevolve","SWEPT_BODY",BODY,{"disambiguationData":[OSD([sQuery(id+"F0.wireOp",EDGE,"E1")])]}),"instanceName":"1"});
            var Q49;
            Q49=makeQuery(id+"F8.opPattern","COPY",BODY,{"derivedFrom":makeQuery(id+"F2.opPattern","COPY",BODY,{"derivedFrom":makeQuery(id+"F1.opRevolve","SWEPT_BODY",BODY,{"disambiguationData":[OSD([sQuery(id+"F0.wireOp",EDGE,"E1")])]}),"instanceName":"1"}),"instanceName":"1"});
            var Q50;
            Q50=makeQuery(id+"F8.opPattern","COPY",BODY,{"derivedFrom":makeQuery(id+"F3.opPattern","COPY",BODY,{"derivedFrom":makeQuery(id+"F2.opPattern","COPY",BODY,{"derivedFrom":makeQuery(id+"F1.opRevolve","SWEPT_BODY",BODY,{"disambiguationData":[OSD([sQuery(id+"F0.wireOp",EDGE,"E1")])]}),"instanceName":"1"}),"instanceName":"1"}),"instanceName":"1"});
            var Q51;
            Q51=makeQuery(id+"F8.opPattern","COPY",BODY,{"derivedFrom":makeQuery(id+"F4.opPattern","COPY",BODY,{"derivedFrom":makeQuery(id+"F1.opRevolve","SWEPT_BODY",BODY,{"disambiguationData":[OSD([sQuery(id+"F0.wireOp",EDGE,"E1")])]}),"instanceName":"1"}),"instanceName":"1"});
            var Q52;
            Q52=makeQuery(id+"F8.opPattern","COPY",BODY,{"derivedFrom":makeQuery(id+"F4.opPattern","COPY",BODY,{"derivedFrom":makeQuery(id+"F2.opPattern","COPY",BODY,{"derivedFrom":makeQuery(id+"F1.opRevolve","SWEPT_BODY",BODY,{"disambiguationData":[OSD([sQuery(id+"F0.wireOp",EDGE,"E1")])]}),"instanceName":"1"}),"instanceName":"1"}),"instanceName":"1"});
            var Q53;
            Q53=makeQuery(id+"F8.opPattern","COPY",BODY,{"derivedFrom":makeQuery(id+"F4.opPattern","COPY",BODY,{"derivedFrom":makeQuery(id+"F3.opPattern","COPY",BODY,{"derivedFrom":makeQuery(id+"F2.opPattern","COPY",BODY,{"derivedFrom":makeQuery(id+"F1.opRevolve","SWEPT_BODY",BODY,{"disambiguationData":[OSD([sQuery(id+"F0.wireOp",EDGE,"E1")])]}),"instanceName":"1"}),"instanceName":"1"}),"instanceName":"1"}),"instanceName":"1"});
            var Q54;
            Q54=makeQuery(id+"F8.opPattern","COPY",BODY,{"derivedFrom":makeQuery(id+"F5.opPattern","COPY",BODY,{"derivedFrom":makeQuery(id+"F1.opRevolve","SWEPT_BODY",BODY,{"disambiguationData":[OSD([sQuery(id+"F0.wireOp",EDGE,"E1")])]}),"instanceName":"1"}),"instanceName":"1"});
            var Q55;
            Q55=makeQuery(id+"F8.opPattern","COPY",BODY,{"derivedFrom":makeQuery(id+"F5.opPattern","COPY",BODY,{"derivedFrom":makeQuery(id+"F2.opPattern","COPY",BODY,{"derivedFrom":makeQuery(id+"F1.opRevolve","SWEPT_BODY",BODY,{"disambiguationData":[OSD([sQuery(id+"F0.wireOp",EDGE,"E1")])]}),"instanceName":"1"}),"instanceName":"1"}),"instanceName":"1"});
            var Q56;
            Q56=makeQuery(id+"F8.opPattern","COPY",BODY,{"derivedFrom":makeQuery(id+"F5.opPattern","COPY",BODY,{"derivedFrom":makeQuery(id+"F3.opPattern","COPY",BODY,{"derivedFrom":makeQuery(id+"F2.opPattern","COPY",BODY,{"derivedFrom":makeQuery(id+"F1.opRevolve","SWEPT_BODY",BODY,{"disambiguationData":[OSD([sQuery(id+"F0.wireOp",EDGE,"E1")])]}),"instanceName":"1"}),"instanceName":"1"}),"instanceName":"1"}),"instanceName":"1"});
            var Q57;
            Q57=makeQuery(id+"F8.opPattern","COPY",BODY,{"derivedFrom":makeQuery(id+"F5.opPattern","COPY",BODY,{"derivedFrom":makeQuery(id+"F4.opPattern","COPY",BODY,{"derivedFrom":makeQuery(id+"F1.opRevolve","SWEPT_BODY",BODY,{"disambiguationData":[OSD([sQuery(id+"F0.wireOp",EDGE,"E1")])]}),"instanceName":"1"}),"instanceName":"1"}),"instanceName":"1"});
            var Q58;
            Q58=makeQuery(id+"F8.opPattern","COPY",BODY,{"derivedFrom":makeQuery(id+"F5.opPattern","COPY",BODY,{"derivedFrom":makeQuery(id+"F4.opPattern","COPY",BODY,{"derivedFrom":makeQuery(id+"F2.opPattern","COPY",BODY,{"derivedFrom":makeQuery(id+"F1.opRevolve","SWEPT_BODY",BODY,{"disambiguationData":[OSD([sQuery(id+"F0.wireOp",EDGE,"E1")])]}),"instanceName":"1"}),"instanceName":"1"}),"instanceName":"1"}),"instanceName":"1"});
            var Q59;
            Q59=makeQuery(id+"F8.opPattern","COPY",BODY,{"derivedFrom":makeQuery(id+"F5.opPattern","COPY",BODY,{"derivedFrom":makeQuery(id+"F4.opPattern","COPY",BODY,{"derivedFrom":makeQuery(id+"F3.opPattern","COPY",BODY,{"derivedFrom":makeQuery(id+"F2.opPattern","COPY",BODY,{"derivedFrom":makeQuery(id+"F1.opRevolve","SWEPT_BODY",BODY,{"disambiguationData":[OSD([sQuery(id+"F0.wireOp",EDGE,"E1")])]}),"instanceName":"1"}),"instanceName":"1"}),"instanceName":"1"}),"instanceName":"1"}),"instanceName":"1"});
            var Q60;
            Q60=makeQuery(id+"F8.opPattern","COPY",BODY,{"derivedFrom":makeQuery(id+"F6.opPattern","COPY",BODY,{"derivedFrom":makeQuery(id+"F1.opRevolve","SWEPT_BODY",BODY,{"disambiguationData":[OSD([sQuery(id+"F0.wireOp",EDGE,"E1")])]}),"instanceName":"1"}),"instanceName":"1"});
            var Q61;
            Q61=makeQuery(id+"F8.opPattern","COPY",BODY,{"derivedFrom":makeQuery(id+"F6.opPattern","COPY",BODY,{"derivedFrom":makeQuery(id+"F2.opPattern","COPY",BODY,{"derivedFrom":makeQuery(id+"F1.opRevolve","SWEPT_BODY",BODY,{"disambiguationData":[OSD([sQuery(id+"F0.wireOp",EDGE,"E1")])]}),"instanceName":"1"}),"instanceName":"1"}),"instanceName":"1"});
            var Q62;
            Q62=makeQuery(id+"F8.opPattern","COPY",BODY,{"derivedFrom":makeQuery(id+"F6.opPattern","COPY",BODY,{"derivedFrom":makeQuery(id+"F3.opPattern","COPY",BODY,{"derivedFrom":makeQuery(id+"F2.opPattern","COPY",BODY,{"derivedFrom":makeQuery(id+"F1.opRevolve","SWEPT_BODY",BODY,{"disambiguationData":[OSD([sQuery(id+"F0.wireOp",EDGE,"E1")])]}),"instanceName":"1"}),"instanceName":"1"}),"instanceName":"1"}),"instanceName":"1"});
            var Q63;
            Q63=makeQuery(id+"F8.opPattern","COPY",BODY,{"derivedFrom":makeQuery(id+"F6.opPattern","COPY",BODY,{"derivedFrom":makeQuery(id+"F4.opPattern","COPY",BODY,{"derivedFrom":makeQuery(id+"F1.opRevolve","SWEPT_BODY",BODY,{"disambiguationData":[OSD([sQuery(id+"F0.wireOp",EDGE,"E1")])]}),"instanceName":"1"}),"instanceName":"1"}),"instanceName":"1"});
            var Q64;
            Q64=makeQuery(id+"F8.opPattern","COPY",BODY,{"derivedFrom":makeQuery(id+"F6.opPattern","COPY",BODY,{"derivedFrom":makeQuery(id+"F4.opPattern","COPY",BODY,{"derivedFrom":makeQuery(id+"F2.opPattern","COPY",BODY,{"derivedFrom":makeQuery(id+"F1.opRevolve","SWEPT_BODY",BODY,{"disambiguationData":[OSD([sQuery(id+"F0.wireOp",EDGE,"E1")])]}),"instanceName":"1"}),"instanceName":"1"}),"instanceName":"1"}),"instanceName":"1"});
            var Q65;
            Q65=makeQuery(id+"F8.opPattern","COPY",BODY,{"derivedFrom":makeQuery(id+"F6.opPattern","COPY",BODY,{"derivedFrom":makeQuery(id+"F4.opPattern","COPY",BODY,{"derivedFrom":makeQuery(id+"F3.opPattern","COPY",BODY,{"derivedFrom":makeQuery(id+"F2.opPattern","COPY",BODY,{"derivedFrom":makeQuery(id+"F1.opRevolve","SWEPT_BODY",BODY,{"disambiguationData":[OSD([sQuery(id+"F0.wireOp",EDGE,"E1")])]}),"instanceName":"1"}),"instanceName":"1"}),"instanceName":"1"}),"instanceName":"1"}),"instanceName":"1"});
            var Q66;
            Q66=makeQuery(id+"F8.opPattern","COPY",BODY,{"derivedFrom":makeQuery(id+"F6.opPattern","COPY",BODY,{"derivedFrom":makeQuery(id+"F5.opPattern","COPY",BODY,{"derivedFrom":makeQuery(id+"F1.opRevolve","SWEPT_BODY",BODY,{"disambiguationData":[OSD([sQuery(id+"F0.wireOp",EDGE,"E1")])]}),"instanceName":"1"}),"instanceName":"1"}),"instanceName":"1"});
            var Q67;
            Q67=makeQuery(id+"F8.opPattern","COPY",BODY,{"derivedFrom":makeQuery(id+"F6.opPattern","COPY",BODY,{"derivedFrom":makeQuery(id+"F5.opPattern","COPY",BODY,{"derivedFrom":makeQuery(id+"F2.opPattern","COPY",BODY,{"derivedFrom":makeQuery(id+"F1.opRevolve","SWEPT_BODY",BODY,{"disambiguationData":[OSD([sQuery(id+"F0.wireOp",EDGE,"E1")])]}),"instanceName":"1"}),"instanceName":"1"}),"instanceName":"1"}),"instanceName":"1"});
            var Q68;
            Q68=makeQuery(id+"F8.opPattern","COPY",BODY,{"derivedFrom":makeQuery(id+"F6.opPattern","COPY",BODY,{"derivedFrom":makeQuery(id+"F5.opPattern","COPY",BODY,{"derivedFrom":makeQuery(id+"F3.opPattern","COPY",BODY,{"derivedFrom":makeQuery(id+"F2.opPattern","COPY",BODY,{"derivedFrom":makeQuery(id+"F1.opRevolve","SWEPT_BODY",BODY,{"disambiguationData":[OSD([sQuery(id+"F0.wireOp",EDGE,"E1")])]}),"instanceName":"1"}),"instanceName":"1"}),"instanceName":"1"}),"instanceName":"1"}),"instanceName":"1"});
            var Q69;
            Q69=makeQuery(id+"F8.opPattern","COPY",BODY,{"derivedFrom":makeQuery(id+"F6.opPattern","COPY",BODY,{"derivedFrom":makeQuery(id+"F5.opPattern","COPY",BODY,{"derivedFrom":makeQuery(id+"F4.opPattern","COPY",BODY,{"derivedFrom":makeQuery(id+"F1.opRevolve","SWEPT_BODY",BODY,{"disambiguationData":[OSD([sQuery(id+"F0.wireOp",EDGE,"E1")])]}),"instanceName":"1"}),"instanceName":"1"}),"instanceName":"1"}),"instanceName":"1"});
            var Q70;
            Q70=makeQuery(id+"F8.opPattern","COPY",BODY,{"derivedFrom":makeQuery(id+"F6.opPattern","COPY",BODY,{"derivedFrom":makeQuery(id+"F5.opPattern","COPY",BODY,{"derivedFrom":makeQuery(id+"F4.opPattern","COPY",BODY,{"derivedFrom":makeQuery(id+"F2.opPattern","COPY",BODY,{"derivedFrom":makeQuery(id+"F1.opRevolve","SWEPT_BODY",BODY,{"disambiguationData":[OSD([sQuery(id+"F0.wireOp",EDGE,"E1")])]}),"instanceName":"1"}),"instanceName":"1"}),"instanceName":"1"}),"instanceName":"1"}),"instanceName":"1"});
            var Q71;
            Q71=makeQuery(id+"F8.opPattern","COPY",BODY,{"derivedFrom":makeQuery(id+"F6.opPattern","COPY",BODY,{"derivedFrom":makeQuery(id+"F5.opPattern","COPY",BODY,{"derivedFrom":makeQuery(id+"F4.opPattern","COPY",BODY,{"derivedFrom":makeQuery(id+"F3.opPattern","COPY",BODY,{"derivedFrom":makeQuery(id+"F2.opPattern","COPY",BODY,{"derivedFrom":makeQuery(id+"F1.opRevolve","SWEPT_BODY",BODY,{"disambiguationData":[OSD([sQuery(id+"F0.wireOp",EDGE,"E1")])]}),"instanceName":"1"}),"instanceName":"1"}),"instanceName":"1"}),"instanceName":"1"}),"instanceName":"1"}),"instanceName":"1"});
            var Q72;
            Q72=makeQuery(id+"F8.opPattern","COPY",BODY,{"derivedFrom":makeQuery(id+"F7.opPattern","COPY",BODY,{"derivedFrom":makeQuery(id+"F1.opRevolve","SWEPT_BODY",BODY,{"disambiguationData":[OSD([sQuery(id+"F0.wireOp",EDGE,"E1")])]}),"instanceName":"1"}),"instanceName":"1"});
            var Q73;
            Q73=makeQuery(id+"F8.opPattern","COPY",BODY,{"derivedFrom":makeQuery(id+"F7.opPattern","COPY",BODY,{"derivedFrom":makeQuery(id+"F2.opPattern","COPY",BODY,{"derivedFrom":makeQuery(id+"F1.opRevolve","SWEPT_BODY",BODY,{"disambiguationData":[OSD([sQuery(id+"F0.wireOp",EDGE,"E1")])]}),"instanceName":"1"}),"instanceName":"1"}),"instanceName":"1"});
            var Q74;
            Q74=makeQuery(id+"F8.opPattern","COPY",BODY,{"derivedFrom":makeQuery(id+"F7.opPattern","COPY",BODY,{"derivedFrom":makeQuery(id+"F3.opPattern","COPY",BODY,{"derivedFrom":makeQuery(id+"F2.opPattern","COPY",BODY,{"derivedFrom":makeQuery(id+"F1.opRevolve","SWEPT_BODY",BODY,{"disambiguationData":[OSD([sQuery(id+"F0.wireOp",EDGE,"E1")])]}),"instanceName":"1"}),"instanceName":"1"}),"instanceName":"1"}),"instanceName":"1"});
            var Q75;
            Q75=makeQuery(id+"F8.opPattern","COPY",BODY,{"derivedFrom":makeQuery(id+"F7.opPattern","COPY",BODY,{"derivedFrom":makeQuery(id+"F4.opPattern","COPY",BODY,{"derivedFrom":makeQuery(id+"F1.opRevolve","SWEPT_BODY",BODY,{"disambiguationData":[OSD([sQuery(id+"F0.wireOp",EDGE,"E1")])]}),"instanceName":"1"}),"instanceName":"1"}),"instanceName":"1"});
            var Q76;
            Q76=makeQuery(id+"F8.opPattern","COPY",BODY,{"derivedFrom":makeQuery(id+"F7.opPattern","COPY",BODY,{"derivedFrom":makeQuery(id+"F4.opPattern","COPY",BODY,{"derivedFrom":makeQuery(id+"F2.opPattern","COPY",BODY,{"derivedFrom":makeQuery(id+"F1.opRevolve","SWEPT_BODY",BODY,{"disambiguationData":[OSD([sQuery(id+"F0.wireOp",EDGE,"E1")])]}),"instanceName":"1"}),"instanceName":"1"}),"instanceName":"1"}),"instanceName":"1"});
            var Q77;
            Q77=makeQuery(id+"F8.opPattern","COPY",BODY,{"derivedFrom":makeQuery(id+"F7.opPattern","COPY",BODY,{"derivedFrom":makeQuery(id+"F4.opPattern","COPY",BODY,{"derivedFrom":makeQuery(id+"F3.opPattern","COPY",BODY,{"derivedFrom":makeQuery(id+"F2.opPattern","COPY",BODY,{"derivedFrom":makeQuery(id+"F1.opRevolve","SWEPT_BODY",BODY,{"disambiguationData":[OSD([sQuery(id+"F0.wireOp",EDGE,"E1")])]}),"instanceName":"1"}),"instanceName":"1"}),"instanceName":"1"}),"instanceName":"1"}),"instanceName":"1"});
            var Q78;
            Q78=makeQuery(id+"F8.opPattern","COPY",BODY,{"derivedFrom":makeQuery(id+"F7.opPattern","COPY",BODY,{"derivedFrom":makeQuery(id+"F5.opPattern","COPY",BODY,{"derivedFrom":makeQuery(id+"F1.opRevolve","SWEPT_BODY",BODY,{"disambiguationData":[OSD([sQuery(id+"F0.wireOp",EDGE,"E1")])]}),"instanceName":"1"}),"instanceName":"1"}),"instanceName":"1"});
            var Q79;
            Q79=makeQuery(id+"F8.opPattern","COPY",BODY,{"derivedFrom":makeQuery(id+"F7.opPattern","COPY",BODY,{"derivedFrom":makeQuery(id+"F5.opPattern","COPY",BODY,{"derivedFrom":makeQuery(id+"F2.opPattern","COPY",BODY,{"derivedFrom":makeQuery(id+"F1.opRevolve","SWEPT_BODY",BODY,{"disambiguationData":[OSD([sQuery(id+"F0.wireOp",EDGE,"E1")])]}),"instanceName":"1"}),"instanceName":"1"}),"instanceName":"1"}),"instanceName":"1"});
            var Q80;
            Q80=makeQuery(id+"F8.opPattern","COPY",BODY,{"derivedFrom":makeQuery(id+"F7.opPattern","COPY",BODY,{"derivedFrom":makeQuery(id+"F5.opPattern","COPY",BODY,{"derivedFrom":makeQuery(id+"F3.opPattern","COPY",BODY,{"derivedFrom":makeQuery(id+"F2.opPattern","COPY",BODY,{"derivedFrom":makeQuery(id+"F1.opRevolve","SWEPT_BODY",BODY,{"disambiguationData":[OSD([sQuery(id+"F0.wireOp",EDGE,"E1")])]}),"instanceName":"1"}),"instanceName":"1"}),"instanceName":"1"}),"instanceName":"1"}),"instanceName":"1"});
            var Q81;
            Q81=makeQuery(id+"F8.opPattern","COPY",BODY,{"derivedFrom":makeQuery(id+"F7.opPattern","COPY",BODY,{"derivedFrom":makeQuery(id+"F5.opPattern","COPY",BODY,{"derivedFrom":makeQuery(id+"F4.opPattern","COPY",BODY,{"derivedFrom":makeQuery(id+"F1.opRevolve","SWEPT_BODY",BODY,{"disambiguationData":[OSD([sQuery(id+"F0.wireOp",EDGE,"E1")])]}),"instanceName":"1"}),"instanceName":"1"}),"instanceName":"1"}),"instanceName":"1"});
            var Q82;
            Q82=makeQuery(id+"F8.opPattern","COPY",BODY,{"derivedFrom":makeQuery(id+"F7.opPattern","COPY",BODY,{"derivedFrom":makeQuery(id+"F5.opPattern","COPY",BODY,{"derivedFrom":makeQuery(id+"F4.opPattern","COPY",BODY,{"derivedFrom":makeQuery(id+"F2.opPattern","COPY",BODY,{"derivedFrom":makeQuery(id+"F1.opRevolve","SWEPT_BODY",BODY,{"disambiguationData":[OSD([sQuery(id+"F0.wireOp",EDGE,"E1")])]}),"instanceName":"1"}),"instanceName":"1"}),"instanceName":"1"}),"instanceName":"1"}),"instanceName":"1"});
            var Q83;
            Q83=makeQuery(id+"F8.opPattern","COPY",BODY,{"derivedFrom":makeQuery(id+"F7.opPattern","COPY",BODY,{"derivedFrom":makeQuery(id+"F5.opPattern","COPY",BODY,{"derivedFrom":makeQuery(id+"F4.opPattern","COPY",BODY,{"derivedFrom":makeQuery(id+"F3.opPattern","COPY",BODY,{"derivedFrom":makeQuery(id+"F2.opPattern","COPY",BODY,{"derivedFrom":makeQuery(id+"F1.opRevolve","SWEPT_BODY",BODY,{"disambiguationData":[OSD([sQuery(id+"F0.wireOp",EDGE,"E1")])]}),"instanceName":"1"}),"instanceName":"1"}),"instanceName":"1"}),"instanceName":"1"}),"instanceName":"1"}),"instanceName":"1"});
            var Q84;
            Q84=makeQuery(id+"F8.opPattern","COPY",BODY,{"derivedFrom":makeQuery(id+"F7.opPattern","COPY",BODY,{"derivedFrom":makeQuery(id+"F6.opPattern","COPY",BODY,{"derivedFrom":makeQuery(id+"F1.opRevolve","SWEPT_BODY",BODY,{"disambiguationData":[OSD([sQuery(id+"F0.wireOp",EDGE,"E1")])]}),"instanceName":"1"}),"instanceName":"1"}),"instanceName":"1"});
            var Q85;
            Q85=makeQuery(id+"F8.opPattern","COPY",BODY,{"derivedFrom":makeQuery(id+"F7.opPattern","COPY",BODY,{"derivedFrom":makeQuery(id+"F6.opPattern","COPY",BODY,{"derivedFrom":makeQuery(id+"F2.opPattern","COPY",BODY,{"derivedFrom":makeQuery(id+"F1.opRevolve","SWEPT_BODY",BODY,{"disambiguationData":[OSD([sQuery(id+"F0.wireOp",EDGE,"E1")])]}),"instanceName":"1"}),"instanceName":"1"}),"instanceName":"1"}),"instanceName":"1"});
            var Q86;
            Q86=makeQuery(id+"F8.opPattern","COPY",BODY,{"derivedFrom":makeQuery(id+"F7.opPattern","COPY",BODY,{"derivedFrom":makeQuery(id+"F6.opPattern","COPY",BODY,{"derivedFrom":makeQuery(id+"F3.opPattern","COPY",BODY,{"derivedFrom":makeQuery(id+"F2.opPattern","COPY",BODY,{"derivedFrom":makeQuery(id+"F1.opRevolve","SWEPT_BODY",BODY,{"disambiguationData":[OSD([sQuery(id+"F0.wireOp",EDGE,"E1")])]}),"instanceName":"1"}),"instanceName":"1"}),"instanceName":"1"}),"instanceName":"1"}),"instanceName":"1"});
            var Q87;
            Q87=makeQuery(id+"F8.opPattern","COPY",BODY,{"derivedFrom":makeQuery(id+"F7.opPattern","COPY",BODY,{"derivedFrom":makeQuery(id+"F6.opPattern","COPY",BODY,{"derivedFrom":makeQuery(id+"F4.opPattern","COPY",BODY,{"derivedFrom":makeQuery(id+"F1.opRevolve","SWEPT_BODY",BODY,{"disambiguationData":[OSD([sQuery(id+"F0.wireOp",EDGE,"E1")])]}),"instanceName":"1"}),"instanceName":"1"}),"instanceName":"1"}),"instanceName":"1"});
            var Q88;
            Q88=makeQuery(id+"F8.opPattern","COPY",BODY,{"derivedFrom":makeQuery(id+"F7.opPattern","COPY",BODY,{"derivedFrom":makeQuery(id+"F6.opPattern","COPY",BODY,{"derivedFrom":makeQuery(id+"F4.opPattern","COPY",BODY,{"derivedFrom":makeQuery(id+"F2.opPattern","COPY",BODY,{"derivedFrom":makeQuery(id+"F1.opRevolve","SWEPT_BODY",BODY,{"disambiguationData":[OSD([sQuery(id+"F0.wireOp",EDGE,"E1")])]}),"instanceName":"1"}),"instanceName":"1"}),"instanceName":"1"}),"instanceName":"1"}),"instanceName":"1"});
            var Q89;
            Q89=makeQuery(id+"F8.opPattern","COPY",BODY,{"derivedFrom":makeQuery(id+"F7.opPattern","COPY",BODY,{"derivedFrom":makeQuery(id+"F6.opPattern","COPY",BODY,{"derivedFrom":makeQuery(id+"F4.opPattern","COPY",BODY,{"derivedFrom":makeQuery(id+"F3.opPattern","COPY",BODY,{"derivedFrom":makeQuery(id+"F2.opPattern","COPY",BODY,{"derivedFrom":makeQuery(id+"F1.opRevolve","SWEPT_BODY",BODY,{"disambiguationData":[OSD([sQuery(id+"F0.wireOp",EDGE,"E1")])]}),"instanceName":"1"}),"instanceName":"1"}),"instanceName":"1"}),"instanceName":"1"}),"instanceName":"1"}),"instanceName":"1"});
            var Q90;
            Q90=makeQuery(id+"F8.opPattern","COPY",BODY,{"derivedFrom":makeQuery(id+"F7.opPattern","COPY",BODY,{"derivedFrom":makeQuery(id+"F6.opPattern","COPY",BODY,{"derivedFrom":makeQuery(id+"F5.opPattern","COPY",BODY,{"derivedFrom":makeQuery(id+"F1.opRevolve","SWEPT_BODY",BODY,{"disambiguationData":[OSD([sQuery(id+"F0.wireOp",EDGE,"E1")])]}),"instanceName":"1"}),"instanceName":"1"}),"instanceName":"1"}),"instanceName":"1"});
            var Q91;
            Q91=makeQuery(id+"F8.opPattern","COPY",BODY,{"derivedFrom":makeQuery(id+"F7.opPattern","COPY",BODY,{"derivedFrom":makeQuery(id+"F6.opPattern","COPY",BODY,{"derivedFrom":makeQuery(id+"F5.opPattern","COPY",BODY,{"derivedFrom":makeQuery(id+"F2.opPattern","COPY",BODY,{"derivedFrom":makeQuery(id+"F1.opRevolve","SWEPT_BODY",BODY,{"disambiguationData":[OSD([sQuery(id+"F0.wireOp",EDGE,"E1")])]}),"instanceName":"1"}),"instanceName":"1"}),"instanceName":"1"}),"instanceName":"1"}),"instanceName":"1"});
            var Q92;
            Q92=makeQuery(id+"F8.opPattern","COPY",BODY,{"derivedFrom":makeQuery(id+"F7.opPattern","COPY",BODY,{"derivedFrom":makeQuery(id+"F6.opPattern","COPY",BODY,{"derivedFrom":makeQuery(id+"F5.opPattern","COPY",BODY,{"derivedFrom":makeQuery(id+"F3.opPattern","COPY",BODY,{"derivedFrom":makeQuery(id+"F2.opPattern","COPY",BODY,{"derivedFrom":makeQuery(id+"F1.opRevolve","SWEPT_BODY",BODY,{"disambiguationData":[OSD([sQuery(id+"F0.wireOp",EDGE,"E1")])]}),"instanceName":"1"}),"instanceName":"1"}),"instanceName":"1"}),"instanceName":"1"}),"instanceName":"1"}),"instanceName":"1"});
            var Q93;
            Q93=makeQuery(id+"F8.opPattern","COPY",BODY,{"derivedFrom":makeQuery(id+"F7.opPattern","COPY",BODY,{"derivedFrom":makeQuery(id+"F6.opPattern","COPY",BODY,{"derivedFrom":makeQuery(id+"F5.opPattern","COPY",BODY,{"derivedFrom":makeQuery(id+"F4.opPattern","COPY",BODY,{"derivedFrom":makeQuery(id+"F1.opRevolve","SWEPT_BODY",BODY,{"disambiguationData":[OSD([sQuery(id+"F0.wireOp",EDGE,"E1")])]}),"instanceName":"1"}),"instanceName":"1"}),"instanceName":"1"}),"instanceName":"1"}),"instanceName":"1"});
            var Q94;
            Q94=makeQuery(id+"F8.opPattern","COPY",BODY,{"derivedFrom":makeQuery(id+"F7.opPattern","COPY",BODY,{"derivedFrom":makeQuery(id+"F6.opPattern","COPY",BODY,{"derivedFrom":makeQuery(id+"F5.opPattern","COPY",BODY,{"derivedFrom":makeQuery(id+"F4.opPattern","COPY",BODY,{"derivedFrom":makeQuery(id+"F2.opPattern","COPY",BODY,{"derivedFrom":makeQuery(id+"F1.opRevolve","SWEPT_BODY",BODY,{"disambiguationData":[OSD([sQuery(id+"F0.wireOp",EDGE,"E1")])]}),"instanceName":"1"}),"instanceName":"1"}),"instanceName":"1"}),"instanceName":"1"}),"instanceName":"1"}),"instanceName":"1"});
            var Q95;
            Q95=makeQuery(id+"F8.opPattern","COPY",BODY,{"derivedFrom":makeQuery(id+"F7.opPattern","COPY",BODY,{"derivedFrom":makeQuery(id+"F6.opPattern","COPY",BODY,{"derivedFrom":makeQuery(id+"F5.opPattern","COPY",BODY,{"derivedFrom":makeQuery(id+"F4.opPattern","COPY",BODY,{"derivedFrom":makeQuery(id+"F3.opPattern","COPY",BODY,{"derivedFrom":makeQuery(id+"F2.opPattern","COPY",BODY,{"derivedFrom":makeQuery(id+"F1.opRevolve","SWEPT_BODY",BODY,{"disambiguationData":[OSD([sQuery(id+"F0.wireOp",EDGE,"E1")])]}),"instanceName":"1"}),"instanceName":"1"}),"instanceName":"1"}),"instanceName":"1"}),"instanceName":"1"}),"instanceName":"1"}),"instanceName":"1"});
            var Q96;
            Q96=makeQuery(id+"F9.opPattern","COPY",BODY,{"derivedFrom":makeQuery(id+"F1.opRevolve","SWEPT_BODY",BODY,{"disambiguationData":[OSD([sQuery(id+"F0.wireOp",EDGE,"E1")])]}),"instanceName":"1"});
            var Q97;
            Q97=makeQuery(id+"F9.opPattern","COPY",BODY,{"derivedFrom":makeQuery(id+"F2.opPattern","COPY",BODY,{"derivedFrom":makeQuery(id+"F1.opRevolve","SWEPT_BODY",BODY,{"disambiguationData":[OSD([sQuery(id+"F0.wireOp",EDGE,"E1")])]}),"instanceName":"1"}),"instanceName":"1"});
            var Q98;
            Q98=makeQuery(id+"F9.opPattern","COPY",BODY,{"derivedFrom":makeQuery(id+"F3.opPattern","COPY",BODY,{"derivedFrom":makeQuery(id+"F2.opPattern","COPY",BODY,{"derivedFrom":makeQuery(id+"F1.opRevolve","SWEPT_BODY",BODY,{"disambiguationData":[OSD([sQuery(id+"F0.wireOp",EDGE,"E1")])]}),"instanceName":"1"}),"instanceName":"1"}),"instanceName":"1"});
            var Q99;
            Q99=makeQuery(id+"F9.opPattern","COPY",BODY,{"derivedFrom":makeQuery(id+"F4.opPattern","COPY",BODY,{"derivedFrom":makeQuery(id+"F1.opRevolve","SWEPT_BODY",BODY,{"disambiguationData":[OSD([sQuery(id+"F0.wireOp",EDGE,"E1")])]}),"instanceName":"1"}),"instanceName":"1"});
            var Q100;
            Q100=makeQuery(id+"F9.opPattern","COPY",BODY,{"derivedFrom":makeQuery(id+"F4.opPattern","COPY",BODY,{"derivedFrom":makeQuery(id+"F2.opPattern","COPY",BODY,{"derivedFrom":makeQuery(id+"F1.opRevolve","SWEPT_BODY",BODY,{"disambiguationData":[OSD([sQuery(id+"F0.wireOp",EDGE,"E1")])]}),"instanceName":"1"}),"instanceName":"1"}),"instanceName":"1"});
            var Q101;
            Q101=makeQuery(id+"F9.opPattern","COPY",BODY,{"derivedFrom":makeQuery(id+"F4.opPattern","COPY",BODY,{"derivedFrom":makeQuery(id+"F3.opPattern","COPY",BODY,{"derivedFrom":makeQuery(id+"F2.opPattern","COPY",BODY,{"derivedFrom":makeQuery(id+"F1.opRevolve","SWEPT_BODY",BODY,{"disambiguationData":[OSD([sQuery(id+"F0.wireOp",EDGE,"E1")])]}),"instanceName":"1"}),"instanceName":"1"}),"instanceName":"1"}),"instanceName":"1"});
            var Q102;
            Q102=makeQuery(id+"F9.opPattern","COPY",BODY,{"derivedFrom":makeQuery(id+"F5.opPattern","COPY",BODY,{"derivedFrom":makeQuery(id+"F1.opRevolve","SWEPT_BODY",BODY,{"disambiguationData":[OSD([sQuery(id+"F0.wireOp",EDGE,"E1")])]}),"instanceName":"1"}),"instanceName":"1"});
            var Q103;
            Q103=makeQuery(id+"F9.opPattern","COPY",BODY,{"derivedFrom":makeQuery(id+"F5.opPattern","COPY",BODY,{"derivedFrom":makeQuery(id+"F2.opPattern","COPY",BODY,{"derivedFrom":makeQuery(id+"F1.opRevolve","SWEPT_BODY",BODY,{"disambiguationData":[OSD([sQuery(id+"F0.wireOp",EDGE,"E1")])]}),"instanceName":"1"}),"instanceName":"1"}),"instanceName":"1"});
            var Q104;
            Q104=makeQuery(id+"F9.opPattern","COPY",BODY,{"derivedFrom":makeQuery(id+"F5.opPattern","COPY",BODY,{"derivedFrom":makeQuery(id+"F3.opPattern","COPY",BODY,{"derivedFrom":makeQuery(id+"F2.opPattern","COPY",BODY,{"derivedFrom":makeQuery(id+"F1.opRevolve","SWEPT_BODY",BODY,{"disambiguationData":[OSD([sQuery(id+"F0.wireOp",EDGE,"E1")])]}),"instanceName":"1"}),"instanceName":"1"}),"instanceName":"1"}),"instanceName":"1"});
            var Q105;
            Q105=makeQuery(id+"F9.opPattern","COPY",BODY,{"derivedFrom":makeQuery(id+"F5.opPattern","COPY",BODY,{"derivedFrom":makeQuery(id+"F4.opPattern","COPY",BODY,{"derivedFrom":makeQuery(id+"F1.opRevolve","SWEPT_BODY",BODY,{"disambiguationData":[OSD([sQuery(id+"F0.wireOp",EDGE,"E1")])]}),"instanceName":"1"}),"instanceName":"1"}),"instanceName":"1"});
            var Q106;
            Q106=makeQuery(id+"F9.opPattern","COPY",BODY,{"derivedFrom":makeQuery(id+"F5.opPattern","COPY",BODY,{"derivedFrom":makeQuery(id+"F4.opPattern","COPY",BODY,{"derivedFrom":makeQuery(id+"F2.opPattern","COPY",BODY,{"derivedFrom":makeQuery(id+"F1.opRevolve","SWEPT_BODY",BODY,{"disambiguationData":[OSD([sQuery(id+"F0.wireOp",EDGE,"E1")])]}),"instanceName":"1"}),"instanceName":"1"}),"instanceName":"1"}),"instanceName":"1"});
            var Q107;
            Q107=makeQuery(id+"F9.opPattern","COPY",BODY,{"derivedFrom":makeQuery(id+"F5.opPattern","COPY",BODY,{"derivedFrom":makeQuery(id+"F4.opPattern","COPY",BODY,{"derivedFrom":makeQuery(id+"F3.opPattern","COPY",BODY,{"derivedFrom":makeQuery(id+"F2.opPattern","COPY",BODY,{"derivedFrom":makeQuery(id+"F1.opRevolve","SWEPT_BODY",BODY,{"disambiguationData":[OSD([sQuery(id+"F0.wireOp",EDGE,"E1")])]}),"instanceName":"1"}),"instanceName":"1"}),"instanceName":"1"}),"instanceName":"1"}),"instanceName":"1"});
            var Q108;
            Q108=makeQuery(id+"F9.opPattern","COPY",BODY,{"derivedFrom":makeQuery(id+"F6.opPattern","COPY",BODY,{"derivedFrom":makeQuery(id+"F1.opRevolve","SWEPT_BODY",BODY,{"disambiguationData":[OSD([sQuery(id+"F0.wireOp",EDGE,"E1")])]}),"instanceName":"1"}),"instanceName":"1"});
            var Q109;
            Q109=makeQuery(id+"F9.opPattern","COPY",BODY,{"derivedFrom":makeQuery(id+"F6.opPattern","COPY",BODY,{"derivedFrom":makeQuery(id+"F2.opPattern","COPY",BODY,{"derivedFrom":makeQuery(id+"F1.opRevolve","SWEPT_BODY",BODY,{"disambiguationData":[OSD([sQuery(id+"F0.wireOp",EDGE,"E1")])]}),"instanceName":"1"}),"instanceName":"1"}),"instanceName":"1"});
            var Q110;
            Q110=makeQuery(id+"F9.opPattern","COPY",BODY,{"derivedFrom":makeQuery(id+"F6.opPattern","COPY",BODY,{"derivedFrom":makeQuery(id+"F3.opPattern","COPY",BODY,{"derivedFrom":makeQuery(id+"F2.opPattern","COPY",BODY,{"derivedFrom":makeQuery(id+"F1.opRevolve","SWEPT_BODY",BODY,{"disambiguationData":[OSD([sQuery(id+"F0.wireOp",EDGE,"E1")])]}),"instanceName":"1"}),"instanceName":"1"}),"instanceName":"1"}),"instanceName":"1"});
            var Q111;
            Q111=makeQuery(id+"F9.opPattern","COPY",BODY,{"derivedFrom":makeQuery(id+"F6.opPattern","COPY",BODY,{"derivedFrom":makeQuery(id+"F4.opPattern","COPY",BODY,{"derivedFrom":makeQuery(id+"F1.opRevolve","SWEPT_BODY",BODY,{"disambiguationData":[OSD([sQuery(id+"F0.wireOp",EDGE,"E1")])]}),"instanceName":"1"}),"instanceName":"1"}),"instanceName":"1"});
            var Q112;
            Q112=makeQuery(id+"F9.opPattern","COPY",BODY,{"derivedFrom":makeQuery(id+"F6.opPattern","COPY",BODY,{"derivedFrom":makeQuery(id+"F4.opPattern","COPY",BODY,{"derivedFrom":makeQuery(id+"F2.opPattern","COPY",BODY,{"derivedFrom":makeQuery(id+"F1.opRevolve","SWEPT_BODY",BODY,{"disambiguationData":[OSD([sQuery(id+"F0.wireOp",EDGE,"E1")])]}),"instanceName":"1"}),"instanceName":"1"}),"instanceName":"1"}),"instanceName":"1"});
            var Q113;
            Q113=makeQuery(id+"F9.opPattern","COPY",BODY,{"derivedFrom":makeQuery(id+"F6.opPattern","COPY",BODY,{"derivedFrom":makeQuery(id+"F4.opPattern","COPY",BODY,{"derivedFrom":makeQuery(id+"F3.opPattern","COPY",BODY,{"derivedFrom":makeQuery(id+"F2.opPattern","COPY",BODY,{"derivedFrom":makeQuery(id+"F1.opRevolve","SWEPT_BODY",BODY,{"disambiguationData":[OSD([sQuery(id+"F0.wireOp",EDGE,"E1")])]}),"instanceName":"1"}),"instanceName":"1"}),"instanceName":"1"}),"instanceName":"1"}),"instanceName":"1"});
            var Q114;
            Q114=makeQuery(id+"F9.opPattern","COPY",BODY,{"derivedFrom":makeQuery(id+"F6.opPattern","COPY",BODY,{"derivedFrom":makeQuery(id+"F5.opPattern","COPY",BODY,{"derivedFrom":makeQuery(id+"F1.opRevolve","SWEPT_BODY",BODY,{"disambiguationData":[OSD([sQuery(id+"F0.wireOp",EDGE,"E1")])]}),"instanceName":"1"}),"instanceName":"1"}),"instanceName":"1"});
            var Q115;
            Q115=makeQuery(id+"F9.opPattern","COPY",BODY,{"derivedFrom":makeQuery(id+"F6.opPattern","COPY",BODY,{"derivedFrom":makeQuery(id+"F5.opPattern","COPY",BODY,{"derivedFrom":makeQuery(id+"F2.opPattern","COPY",BODY,{"derivedFrom":makeQuery(id+"F1.opRevolve","SWEPT_BODY",BODY,{"disambiguationData":[OSD([sQuery(id+"F0.wireOp",EDGE,"E1")])]}),"instanceName":"1"}),"instanceName":"1"}),"instanceName":"1"}),"instanceName":"1"});
            var Q116;
            Q116=makeQuery(id+"F9.opPattern","COPY",BODY,{"derivedFrom":makeQuery(id+"F6.opPattern","COPY",BODY,{"derivedFrom":makeQuery(id+"F5.opPattern","COPY",BODY,{"derivedFrom":makeQuery(id+"F3.opPattern","COPY",BODY,{"derivedFrom":makeQuery(id+"F2.opPattern","COPY",BODY,{"derivedFrom":makeQuery(id+"F1.opRevolve","SWEPT_BODY",BODY,{"disambiguationData":[OSD([sQuery(id+"F0.wireOp",EDGE,"E1")])]}),"instanceName":"1"}),"instanceName":"1"}),"instanceName":"1"}),"instanceName":"1"}),"instanceName":"1"});
            var Q117;
            Q117=makeQuery(id+"F9.opPattern","COPY",BODY,{"derivedFrom":makeQuery(id+"F6.opPattern","COPY",BODY,{"derivedFrom":makeQuery(id+"F5.opPattern","COPY",BODY,{"derivedFrom":makeQuery(id+"F4.opPattern","COPY",BODY,{"derivedFrom":makeQuery(id+"F1.opRevolve","SWEPT_BODY",BODY,{"disambiguationData":[OSD([sQuery(id+"F0.wireOp",EDGE,"E1")])]}),"instanceName":"1"}),"instanceName":"1"}),"instanceName":"1"}),"instanceName":"1"});
            var Q118;
            Q118=makeQuery(id+"F9.opPattern","COPY",BODY,{"derivedFrom":makeQuery(id+"F6.opPattern","COPY",BODY,{"derivedFrom":makeQuery(id+"F5.opPattern","COPY",BODY,{"derivedFrom":makeQuery(id+"F4.opPattern","COPY",BODY,{"derivedFrom":makeQuery(id+"F2.opPattern","COPY",BODY,{"derivedFrom":makeQuery(id+"F1.opRevolve","SWEPT_BODY",BODY,{"disambiguationData":[OSD([sQuery(id+"F0.wireOp",EDGE,"E1")])]}),"instanceName":"1"}),"instanceName":"1"}),"instanceName":"1"}),"instanceName":"1"}),"instanceName":"1"});
            var Q119;
            Q119=makeQuery(id+"F9.opPattern","COPY",BODY,{"derivedFrom":makeQuery(id+"F6.opPattern","COPY",BODY,{"derivedFrom":makeQuery(id+"F5.opPattern","COPY",BODY,{"derivedFrom":makeQuery(id+"F4.opPattern","COPY",BODY,{"derivedFrom":makeQuery(id+"F3.opPattern","COPY",BODY,{"derivedFrom":makeQuery(id+"F2.opPattern","COPY",BODY,{"derivedFrom":makeQuery(id+"F1.opRevolve","SWEPT_BODY",BODY,{"disambiguationData":[OSD([sQuery(id+"F0.wireOp",EDGE,"E1")])]}),"instanceName":"1"}),"instanceName":"1"}),"instanceName":"1"}),"instanceName":"1"}),"instanceName":"1"}),"instanceName":"1"});
            var Q120;
            Q120=makeQuery(id+"F9.opPattern","COPY",BODY,{"derivedFrom":makeQuery(id+"F7.opPattern","COPY",BODY,{"derivedFrom":makeQuery(id+"F1.opRevolve","SWEPT_BODY",BODY,{"disambiguationData":[OSD([sQuery(id+"F0.wireOp",EDGE,"E1")])]}),"instanceName":"1"}),"instanceName":"1"});
            var Q121;
            Q121=makeQuery(id+"F9.opPattern","COPY",BODY,{"derivedFrom":makeQuery(id+"F7.opPattern","COPY",BODY,{"derivedFrom":makeQuery(id+"F2.opPattern","COPY",BODY,{"derivedFrom":makeQuery(id+"F1.opRevolve","SWEPT_BODY",BODY,{"disambiguationData":[OSD([sQuery(id+"F0.wireOp",EDGE,"E1")])]}),"instanceName":"1"}),"instanceName":"1"}),"instanceName":"1"});
            var Q122;
            Q122=makeQuery(id+"F9.opPattern","COPY",BODY,{"derivedFrom":makeQuery(id+"F7.opPattern","COPY",BODY,{"derivedFrom":makeQuery(id+"F3.opPattern","COPY",BODY,{"derivedFrom":makeQuery(id+"F2.opPattern","COPY",BODY,{"derivedFrom":makeQuery(id+"F1.opRevolve","SWEPT_BODY",BODY,{"disambiguationData":[OSD([sQuery(id+"F0.wireOp",EDGE,"E1")])]}),"instanceName":"1"}),"instanceName":"1"}),"instanceName":"1"}),"instanceName":"1"});
            var Q123;
            Q123=makeQuery(id+"F9.opPattern","COPY",BODY,{"derivedFrom":makeQuery(id+"F7.opPattern","COPY",BODY,{"derivedFrom":makeQuery(id+"F4.opPattern","COPY",BODY,{"derivedFrom":makeQuery(id+"F1.opRevolve","SWEPT_BODY",BODY,{"disambiguationData":[OSD([sQuery(id+"F0.wireOp",EDGE,"E1")])]}),"instanceName":"1"}),"instanceName":"1"}),"instanceName":"1"});
            var Q124;
            Q124=makeQuery(id+"F9.opPattern","COPY",BODY,{"derivedFrom":makeQuery(id+"F7.opPattern","COPY",BODY,{"derivedFrom":makeQuery(id+"F4.opPattern","COPY",BODY,{"derivedFrom":makeQuery(id+"F2.opPattern","COPY",BODY,{"derivedFrom":makeQuery(id+"F1.opRevolve","SWEPT_BODY",BODY,{"disambiguationData":[OSD([sQuery(id+"F0.wireOp",EDGE,"E1")])]}),"instanceName":"1"}),"instanceName":"1"}),"instanceName":"1"}),"instanceName":"1"});
            var Q125;
            Q125=makeQuery(id+"F9.opPattern","COPY",BODY,{"derivedFrom":makeQuery(id+"F7.opPattern","COPY",BODY,{"derivedFrom":makeQuery(id+"F4.opPattern","COPY",BODY,{"derivedFrom":makeQuery(id+"F3.opPattern","COPY",BODY,{"derivedFrom":makeQuery(id+"F2.opPattern","COPY",BODY,{"derivedFrom":makeQuery(id+"F1.opRevolve","SWEPT_BODY",BODY,{"disambiguationData":[OSD([sQuery(id+"F0.wireOp",EDGE,"E1")])]}),"instanceName":"1"}),"instanceName":"1"}),"instanceName":"1"}),"instanceName":"1"}),"instanceName":"1"});
            var Q126;
            Q126=makeQuery(id+"F9.opPattern","COPY",BODY,{"derivedFrom":makeQuery(id+"F7.opPattern","COPY",BODY,{"derivedFrom":makeQuery(id+"F5.opPattern","COPY",BODY,{"derivedFrom":makeQuery(id+"F1.opRevolve","SWEPT_BODY",BODY,{"disambiguationData":[OSD([sQuery(id+"F0.wireOp",EDGE,"E1")])]}),"instanceName":"1"}),"instanceName":"1"}),"instanceName":"1"});
            var Q127;
            Q127=makeQuery(id+"F9.opPattern","COPY",BODY,{"derivedFrom":makeQuery(id+"F7.opPattern","COPY",BODY,{"derivedFrom":makeQuery(id+"F5.opPattern","COPY",BODY,{"derivedFrom":makeQuery(id+"F2.opPattern","COPY",BODY,{"derivedFrom":makeQuery(id+"F1.opRevolve","SWEPT_BODY",BODY,{"disambiguationData":[OSD([sQuery(id+"F0.wireOp",EDGE,"E1")])]}),"instanceName":"1"}),"instanceName":"1"}),"instanceName":"1"}),"instanceName":"1"});
            var Q128;
            Q128=makeQuery(id+"F9.opPattern","COPY",BODY,{"derivedFrom":makeQuery(id+"F7.opPattern","COPY",BODY,{"derivedFrom":makeQuery(id+"F5.opPattern","COPY",BODY,{"derivedFrom":makeQuery(id+"F3.opPattern","COPY",BODY,{"derivedFrom":makeQuery(id+"F2.opPattern","COPY",BODY,{"derivedFrom":makeQuery(id+"F1.opRevolve","SWEPT_BODY",BODY,{"disambiguationData":[OSD([sQuery(id+"F0.wireOp",EDGE,"E1")])]}),"instanceName":"1"}),"instanceName":"1"}),"instanceName":"1"}),"instanceName":"1"}),"instanceName":"1"});
            var Q129;
            Q129=makeQuery(id+"F9.opPattern","COPY",BODY,{"derivedFrom":makeQuery(id+"F7.opPattern","COPY",BODY,{"derivedFrom":makeQuery(id+"F5.opPattern","COPY",BODY,{"derivedFrom":makeQuery(id+"F4.opPattern","COPY",BODY,{"derivedFrom":makeQuery(id+"F1.opRevolve","SWEPT_BODY",BODY,{"disambiguationData":[OSD([sQuery(id+"F0.wireOp",EDGE,"E1")])]}),"instanceName":"1"}),"instanceName":"1"}),"instanceName":"1"}),"instanceName":"1"});
            var Q130;
            Q130=makeQuery(id+"F9.opPattern","COPY",BODY,{"derivedFrom":makeQuery(id+"F7.opPattern","COPY",BODY,{"derivedFrom":makeQuery(id+"F5.opPattern","COPY",BODY,{"derivedFrom":makeQuery(id+"F4.opPattern","COPY",BODY,{"derivedFrom":makeQuery(id+"F2.opPattern","COPY",BODY,{"derivedFrom":makeQuery(id+"F1.opRevolve","SWEPT_BODY",BODY,{"disambiguationData":[OSD([sQuery(id+"F0.wireOp",EDGE,"E1")])]}),"instanceName":"1"}),"instanceName":"1"}),"instanceName":"1"}),"instanceName":"1"}),"instanceName":"1"});
            var Q131;
            Q131=makeQuery(id+"F9.opPattern","COPY",BODY,{"derivedFrom":makeQuery(id+"F7.opPattern","COPY",BODY,{"derivedFrom":makeQuery(id+"F5.opPattern","COPY",BODY,{"derivedFrom":makeQuery(id+"F4.opPattern","COPY",BODY,{"derivedFrom":makeQuery(id+"F3.opPattern","COPY",BODY,{"derivedFrom":makeQuery(id+"F2.opPattern","COPY",BODY,{"derivedFrom":makeQuery(id+"F1.opRevolve","SWEPT_BODY",BODY,{"disambiguationData":[OSD([sQuery(id+"F0.wireOp",EDGE,"E1")])]}),"instanceName":"1"}),"instanceName":"1"}),"instanceName":"1"}),"instanceName":"1"}),"instanceName":"1"}),"instanceName":"1"});
            var Q132;
            Q132=makeQuery(id+"F9.opPattern","COPY",BODY,{"derivedFrom":makeQuery(id+"F7.opPattern","COPY",BODY,{"derivedFrom":makeQuery(id+"F6.opPattern","COPY",BODY,{"derivedFrom":makeQuery(id+"F1.opRevolve","SWEPT_BODY",BODY,{"disambiguationData":[OSD([sQuery(id+"F0.wireOp",EDGE,"E1")])]}),"instanceName":"1"}),"instanceName":"1"}),"instanceName":"1"});
            var Q133;
            Q133=makeQuery(id+"F9.opPattern","COPY",BODY,{"derivedFrom":makeQuery(id+"F7.opPattern","COPY",BODY,{"derivedFrom":makeQuery(id+"F6.opPattern","COPY",BODY,{"derivedFrom":makeQuery(id+"F2.opPattern","COPY",BODY,{"derivedFrom":makeQuery(id+"F1.opRevolve","SWEPT_BODY",BODY,{"disambiguationData":[OSD([sQuery(id+"F0.wireOp",EDGE,"E1")])]}),"instanceName":"1"}),"instanceName":"1"}),"instanceName":"1"}),"instanceName":"1"});
            var Q134;
            Q134=makeQuery(id+"F9.opPattern","COPY",BODY,{"derivedFrom":makeQuery(id+"F7.opPattern","COPY",BODY,{"derivedFrom":makeQuery(id+"F6.opPattern","COPY",BODY,{"derivedFrom":makeQuery(id+"F3.opPattern","COPY",BODY,{"derivedFrom":makeQuery(id+"F2.opPattern","COPY",BODY,{"derivedFrom":makeQuery(id+"F1.opRevolve","SWEPT_BODY",BODY,{"disambiguationData":[OSD([sQuery(id+"F0.wireOp",EDGE,"E1")])]}),"instanceName":"1"}),"instanceName":"1"}),"instanceName":"1"}),"instanceName":"1"}),"instanceName":"1"});
            var Q135;
            Q135=makeQuery(id+"F9.opPattern","COPY",BODY,{"derivedFrom":makeQuery(id+"F7.opPattern","COPY",BODY,{"derivedFrom":makeQuery(id+"F6.opPattern","COPY",BODY,{"derivedFrom":makeQuery(id+"F4.opPattern","COPY",BODY,{"derivedFrom":makeQuery(id+"F1.opRevolve","SWEPT_BODY",BODY,{"disambiguationData":[OSD([sQuery(id+"F0.wireOp",EDGE,"E1")])]}),"instanceName":"1"}),"instanceName":"1"}),"instanceName":"1"}),"instanceName":"1"});
            var Q136;
            Q136=makeQuery(id+"F9.opPattern","COPY",BODY,{"derivedFrom":makeQuery(id+"F7.opPattern","COPY",BODY,{"derivedFrom":makeQuery(id+"F6.opPattern","COPY",BODY,{"derivedFrom":makeQuery(id+"F4.opPattern","COPY",BODY,{"derivedFrom":makeQuery(id+"F2.opPattern","COPY",BODY,{"derivedFrom":makeQuery(id+"F1.opRevolve","SWEPT_BODY",BODY,{"disambiguationData":[OSD([sQuery(id+"F0.wireOp",EDGE,"E1")])]}),"instanceName":"1"}),"instanceName":"1"}),"instanceName":"1"}),"instanceName":"1"}),"instanceName":"1"});
            var Q137;
            Q137=makeQuery(id+"F9.opPattern","COPY",BODY,{"derivedFrom":makeQuery(id+"F7.opPattern","COPY",BODY,{"derivedFrom":makeQuery(id+"F6.opPattern","COPY",BODY,{"derivedFrom":makeQuery(id+"F4.opPattern","COPY",BODY,{"derivedFrom":makeQuery(id+"F3.opPattern","COPY",BODY,{"derivedFrom":makeQuery(id+"F2.opPattern","COPY",BODY,{"derivedFrom":makeQuery(id+"F1.opRevolve","SWEPT_BODY",BODY,{"disambiguationData":[OSD([sQuery(id+"F0.wireOp",EDGE,"E1")])]}),"instanceName":"1"}),"instanceName":"1"}),"instanceName":"1"}),"instanceName":"1"}),"instanceName":"1"}),"instanceName":"1"});
            var Q138;
            Q138=makeQuery(id+"F9.opPattern","COPY",BODY,{"derivedFrom":makeQuery(id+"F7.opPattern","COPY",BODY,{"derivedFrom":makeQuery(id+"F6.opPattern","COPY",BODY,{"derivedFrom":makeQuery(id+"F5.opPattern","COPY",BODY,{"derivedFrom":makeQuery(id+"F1.opRevolve","SWEPT_BODY",BODY,{"disambiguationData":[OSD([sQuery(id+"F0.wireOp",EDGE,"E1")])]}),"instanceName":"1"}),"instanceName":"1"}),"instanceName":"1"}),"instanceName":"1"});
            var Q139;
            Q139=makeQuery(id+"F9.opPattern","COPY",BODY,{"derivedFrom":makeQuery(id+"F7.opPattern","COPY",BODY,{"derivedFrom":makeQuery(id+"F6.opPattern","COPY",BODY,{"derivedFrom":makeQuery(id+"F5.opPattern","COPY",BODY,{"derivedFrom":makeQuery(id+"F2.opPattern","COPY",BODY,{"derivedFrom":makeQuery(id+"F1.opRevolve","SWEPT_BODY",BODY,{"disambiguationData":[OSD([sQuery(id+"F0.wireOp",EDGE,"E1")])]}),"instanceName":"1"}),"instanceName":"1"}),"instanceName":"1"}),"instanceName":"1"}),"instanceName":"1"});
            var Q140;
            Q140=makeQuery(id+"F9.opPattern","COPY",BODY,{"derivedFrom":makeQuery(id+"F7.opPattern","COPY",BODY,{"derivedFrom":makeQuery(id+"F6.opPattern","COPY",BODY,{"derivedFrom":makeQuery(id+"F5.opPattern","COPY",BODY,{"derivedFrom":makeQuery(id+"F3.opPattern","COPY",BODY,{"derivedFrom":makeQuery(id+"F2.opPattern","COPY",BODY,{"derivedFrom":makeQuery(id+"F1.opRevolve","SWEPT_BODY",BODY,{"disambiguationData":[OSD([sQuery(id+"F0.wireOp",EDGE,"E1")])]}),"instanceName":"1"}),"instanceName":"1"}),"instanceName":"1"}),"instanceName":"1"}),"instanceName":"1"}),"instanceName":"1"});
            var Q141;
            Q141=makeQuery(id+"F9.opPattern","COPY",BODY,{"derivedFrom":makeQuery(id+"F7.opPattern","COPY",BODY,{"derivedFrom":makeQuery(id+"F6.opPattern","COPY",BODY,{"derivedFrom":makeQuery(id+"F5.opPattern","COPY",BODY,{"derivedFrom":makeQuery(id+"F4.opPattern","COPY",BODY,{"derivedFrom":makeQuery(id+"F1.opRevolve","SWEPT_BODY",BODY,{"disambiguationData":[OSD([sQuery(id+"F0.wireOp",EDGE,"E1")])]}),"instanceName":"1"}),"instanceName":"1"}),"instanceName":"1"}),"instanceName":"1"}),"instanceName":"1"});
            var Q142;
            Q142=makeQuery(id+"F9.opPattern","COPY",BODY,{"derivedFrom":makeQuery(id+"F7.opPattern","COPY",BODY,{"derivedFrom":makeQuery(id+"F6.opPattern","COPY",BODY,{"derivedFrom":makeQuery(id+"F5.opPattern","COPY",BODY,{"derivedFrom":makeQuery(id+"F4.opPattern","COPY",BODY,{"derivedFrom":makeQuery(id+"F2.opPattern","COPY",BODY,{"derivedFrom":makeQuery(id+"F1.opRevolve","SWEPT_BODY",BODY,{"disambiguationData":[OSD([sQuery(id+"F0.wireOp",EDGE,"E1")])]}),"instanceName":"1"}),"instanceName":"1"}),"instanceName":"1"}),"instanceName":"1"}),"instanceName":"1"}),"instanceName":"1"});
            var Q143;
            Q143=makeQuery(id+"F9.opPattern","COPY",BODY,{"derivedFrom":makeQuery(id+"F7.opPattern","COPY",BODY,{"derivedFrom":makeQuery(id+"F6.opPattern","COPY",BODY,{"derivedFrom":makeQuery(id+"F5.opPattern","COPY",BODY,{"derivedFrom":makeQuery(id+"F4.opPattern","COPY",BODY,{"derivedFrom":makeQuery(id+"F3.opPattern","COPY",BODY,{"derivedFrom":makeQuery(id+"F2.opPattern","COPY",BODY,{"derivedFrom":makeQuery(id+"F1.opRevolve","SWEPT_BODY",BODY,{"disambiguationData":[OSD([sQuery(id+"F0.wireOp",EDGE,"E1")])]}),"instanceName":"1"}),"instanceName":"1"}),"instanceName":"1"}),"instanceName":"1"}),"instanceName":"1"}),"instanceName":"1"}),"instanceName":"1"});
            var Q144;
            Q144=makeQuery(id+"F9.opPattern","COPY",BODY,{"derivedFrom":makeQuery(id+"F8.opPattern","COPY",BODY,{"derivedFrom":makeQuery(id+"F1.opRevolve","SWEPT_BODY",BODY,{"disambiguationData":[OSD([sQuery(id+"F0.wireOp",EDGE,"E1")])]}),"instanceName":"1"}),"instanceName":"1"});
            var Q145;
            Q145=makeQuery(id+"F9.opPattern","COPY",BODY,{"derivedFrom":makeQuery(id+"F8.opPattern","COPY",BODY,{"derivedFrom":makeQuery(id+"F2.opPattern","COPY",BODY,{"derivedFrom":makeQuery(id+"F1.opRevolve","SWEPT_BODY",BODY,{"disambiguationData":[OSD([sQuery(id+"F0.wireOp",EDGE,"E1")])]}),"instanceName":"1"}),"instanceName":"1"}),"instanceName":"1"});
            var Q146;
            Q146=makeQuery(id+"F9.opPattern","COPY",BODY,{"derivedFrom":makeQuery(id+"F8.opPattern","COPY",BODY,{"derivedFrom":makeQuery(id+"F3.opPattern","COPY",BODY,{"derivedFrom":makeQuery(id+"F2.opPattern","COPY",BODY,{"derivedFrom":makeQuery(id+"F1.opRevolve","SWEPT_BODY",BODY,{"disambiguationData":[OSD([sQuery(id+"F0.wireOp",EDGE,"E1")])]}),"instanceName":"1"}),"instanceName":"1"}),"instanceName":"1"}),"instanceName":"1"});
            var Q147;
            Q147=makeQuery(id+"F9.opPattern","COPY",BODY,{"derivedFrom":makeQuery(id+"F8.opPattern","COPY",BODY,{"derivedFrom":makeQuery(id+"F4.opPattern","COPY",BODY,{"derivedFrom":makeQuery(id+"F1.opRevolve","SWEPT_BODY",BODY,{"disambiguationData":[OSD([sQuery(id+"F0.wireOp",EDGE,"E1")])]}),"instanceName":"1"}),"instanceName":"1"}),"instanceName":"1"});
            var Q148;
            Q148=makeQuery(id+"F9.opPattern","COPY",BODY,{"derivedFrom":makeQuery(id+"F8.opPattern","COPY",BODY,{"derivedFrom":makeQuery(id+"F4.opPattern","COPY",BODY,{"derivedFrom":makeQuery(id+"F2.opPattern","COPY",BODY,{"derivedFrom":makeQuery(id+"F1.opRevolve","SWEPT_BODY",BODY,{"disambiguationData":[OSD([sQuery(id+"F0.wireOp",EDGE,"E1")])]}),"instanceName":"1"}),"instanceName":"1"}),"instanceName":"1"}),"instanceName":"1"});
            var Q149;
            Q149=makeQuery(id+"F9.opPattern","COPY",BODY,{"derivedFrom":makeQuery(id+"F8.opPattern","COPY",BODY,{"derivedFrom":makeQuery(id+"F4.opPattern","COPY",BODY,{"derivedFrom":makeQuery(id+"F3.opPattern","COPY",BODY,{"derivedFrom":makeQuery(id+"F2.opPattern","COPY",BODY,{"derivedFrom":makeQuery(id+"F1.opRevolve","SWEPT_BODY",BODY,{"disambiguationData":[OSD([sQuery(id+"F0.wireOp",EDGE,"E1")])]}),"instanceName":"1"}),"instanceName":"1"}),"instanceName":"1"}),"instanceName":"1"}),"instanceName":"1"});
            var Q150;
            Q150=makeQuery(id+"F9.opPattern","COPY",BODY,{"derivedFrom":makeQuery(id+"F8.opPattern","COPY",BODY,{"derivedFrom":makeQuery(id+"F5.opPattern","COPY",BODY,{"derivedFrom":makeQuery(id+"F1.opRevolve","SWEPT_BODY",BODY,{"disambiguationData":[OSD([sQuery(id+"F0.wireOp",EDGE,"E1")])]}),"instanceName":"1"}),"instanceName":"1"}),"instanceName":"1"});
            var Q151;
            Q151=makeQuery(id+"F9.opPattern","COPY",BODY,{"derivedFrom":makeQuery(id+"F8.opPattern","COPY",BODY,{"derivedFrom":makeQuery(id+"F5.opPattern","COPY",BODY,{"derivedFrom":makeQuery(id+"F2.opPattern","COPY",BODY,{"derivedFrom":makeQuery(id+"F1.opRevolve","SWEPT_BODY",BODY,{"disambiguationData":[OSD([sQuery(id+"F0.wireOp",EDGE,"E1")])]}),"instanceName":"1"}),"instanceName":"1"}),"instanceName":"1"}),"instanceName":"1"});
            var Q152;
            Q152=makeQuery(id+"F9.opPattern","COPY",BODY,{"derivedFrom":makeQuery(id+"F8.opPattern","COPY",BODY,{"derivedFrom":makeQuery(id+"F5.opPattern","COPY",BODY,{"derivedFrom":makeQuery(id+"F3.opPattern","COPY",BODY,{"derivedFrom":makeQuery(id+"F2.opPattern","COPY",BODY,{"derivedFrom":makeQuery(id+"F1.opRevolve","SWEPT_BODY",BODY,{"disambiguationData":[OSD([sQuery(id+"F0.wireOp",EDGE,"E1")])]}),"instanceName":"1"}),"instanceName":"1"}),"instanceName":"1"}),"instanceName":"1"}),"instanceName":"1"});
            var Q153;
            Q153=makeQuery(id+"F9.opPattern","COPY",BODY,{"derivedFrom":makeQuery(id+"F8.opPattern","COPY",BODY,{"derivedFrom":makeQuery(id+"F5.opPattern","COPY",BODY,{"derivedFrom":makeQuery(id+"F4.opPattern","COPY",BODY,{"derivedFrom":makeQuery(id+"F1.opRevolve","SWEPT_BODY",BODY,{"disambiguationData":[OSD([sQuery(id+"F0.wireOp",EDGE,"E1")])]}),"instanceName":"1"}),"instanceName":"1"}),"instanceName":"1"}),"instanceName":"1"});
            var Q154;
            Q154=makeQuery(id+"F9.opPattern","COPY",BODY,{"derivedFrom":makeQuery(id+"F8.opPattern","COPY",BODY,{"derivedFrom":makeQuery(id+"F5.opPattern","COPY",BODY,{"derivedFrom":makeQuery(id+"F4.opPattern","COPY",BODY,{"derivedFrom":makeQuery(id+"F2.opPattern","COPY",BODY,{"derivedFrom":makeQuery(id+"F1.opRevolve","SWEPT_BODY",BODY,{"disambiguationData":[OSD([sQuery(id+"F0.wireOp",EDGE,"E1")])]}),"instanceName":"1"}),"instanceName":"1"}),"instanceName":"1"}),"instanceName":"1"}),"instanceName":"1"});
            var Q155;
            Q155=makeQuery(id+"F9.opPattern","COPY",BODY,{"derivedFrom":makeQuery(id+"F8.opPattern","COPY",BODY,{"derivedFrom":makeQuery(id+"F5.opPattern","COPY",BODY,{"derivedFrom":makeQuery(id+"F4.opPattern","COPY",BODY,{"derivedFrom":makeQuery(id+"F3.opPattern","COPY",BODY,{"derivedFrom":makeQuery(id+"F2.opPattern","COPY",BODY,{"derivedFrom":makeQuery(id+"F1.opRevolve","SWEPT_BODY",BODY,{"disambiguationData":[OSD([sQuery(id+"F0.wireOp",EDGE,"E1")])]}),"instanceName":"1"}),"instanceName":"1"}),"instanceName":"1"}),"instanceName":"1"}),"instanceName":"1"}),"instanceName":"1"});
            var Q156;
            Q156=makeQuery(id+"F9.opPattern","COPY",BODY,{"derivedFrom":makeQuery(id+"F8.opPattern","COPY",BODY,{"derivedFrom":makeQuery(id+"F6.opPattern","COPY",BODY,{"derivedFrom":makeQuery(id+"F1.opRevolve","SWEPT_BODY",BODY,{"disambiguationData":[OSD([sQuery(id+"F0.wireOp",EDGE,"E1")])]}),"instanceName":"1"}),"instanceName":"1"}),"instanceName":"1"});
            var Q157;
            Q157=makeQuery(id+"F9.opPattern","COPY",BODY,{"derivedFrom":makeQuery(id+"F8.opPattern","COPY",BODY,{"derivedFrom":makeQuery(id+"F6.opPattern","COPY",BODY,{"derivedFrom":makeQuery(id+"F2.opPattern","COPY",BODY,{"derivedFrom":makeQuery(id+"F1.opRevolve","SWEPT_BODY",BODY,{"disambiguationData":[OSD([sQuery(id+"F0.wireOp",EDGE,"E1")])]}),"instanceName":"1"}),"instanceName":"1"}),"instanceName":"1"}),"instanceName":"1"});
            var Q158;
            Q158=makeQuery(id+"F9.opPattern","COPY",BODY,{"derivedFrom":makeQuery(id+"F8.opPattern","COPY",BODY,{"derivedFrom":makeQuery(id+"F6.opPattern","COPY",BODY,{"derivedFrom":makeQuery(id+"F3.opPattern","COPY",BODY,{"derivedFrom":makeQuery(id+"F2.opPattern","COPY",BODY,{"derivedFrom":makeQuery(id+"F1.opRevolve","SWEPT_BODY",BODY,{"disambiguationData":[OSD([sQuery(id+"F0.wireOp",EDGE,"E1")])]}),"instanceName":"1"}),"instanceName":"1"}),"instanceName":"1"}),"instanceName":"1"}),"instanceName":"1"});
            var Q159;
            Q159=makeQuery(id+"F9.opPattern","COPY",BODY,{"derivedFrom":makeQuery(id+"F8.opPattern","COPY",BODY,{"derivedFrom":makeQuery(id+"F6.opPattern","COPY",BODY,{"derivedFrom":makeQuery(id+"F4.opPattern","COPY",BODY,{"derivedFrom":makeQuery(id+"F1.opRevolve","SWEPT_BODY",BODY,{"disambiguationData":[OSD([sQuery(id+"F0.wireOp",EDGE,"E1")])]}),"instanceName":"1"}),"instanceName":"1"}),"instanceName":"1"}),"instanceName":"1"});
            var Q160;
            Q160=makeQuery(id+"F9.opPattern","COPY",BODY,{"derivedFrom":makeQuery(id+"F8.opPattern","COPY",BODY,{"derivedFrom":makeQuery(id+"F6.opPattern","COPY",BODY,{"derivedFrom":makeQuery(id+"F4.opPattern","COPY",BODY,{"derivedFrom":makeQuery(id+"F2.opPattern","COPY",BODY,{"derivedFrom":makeQuery(id+"F1.opRevolve","SWEPT_BODY",BODY,{"disambiguationData":[OSD([sQuery(id+"F0.wireOp",EDGE,"E1")])]}),"instanceName":"1"}),"instanceName":"1"}),"instanceName":"1"}),"instanceName":"1"}),"instanceName":"1"});
            var Q161;
            Q161=makeQuery(id+"F9.opPattern","COPY",BODY,{"derivedFrom":makeQuery(id+"F8.opPattern","COPY",BODY,{"derivedFrom":makeQuery(id+"F6.opPattern","COPY",BODY,{"derivedFrom":makeQuery(id+"F4.opPattern","COPY",BODY,{"derivedFrom":makeQuery(id+"F3.opPattern","COPY",BODY,{"derivedFrom":makeQuery(id+"F2.opPattern","COPY",BODY,{"derivedFrom":makeQuery(id+"F1.opRevolve","SWEPT_BODY",BODY,{"disambiguationData":[OSD([sQuery(id+"F0.wireOp",EDGE,"E1")])]}),"instanceName":"1"}),"instanceName":"1"}),"instanceName":"1"}),"instanceName":"1"}),"instanceName":"1"}),"instanceName":"1"});
            var Q162;
            Q162=makeQuery(id+"F9.opPattern","COPY",BODY,{"derivedFrom":makeQuery(id+"F8.opPattern","COPY",BODY,{"derivedFrom":makeQuery(id+"F6.opPattern","COPY",BODY,{"derivedFrom":makeQuery(id+"F5.opPattern","COPY",BODY,{"derivedFrom":makeQuery(id+"F1.opRevolve","SWEPT_BODY",BODY,{"disambiguationData":[OSD([sQuery(id+"F0.wireOp",EDGE,"E1")])]}),"instanceName":"1"}),"instanceName":"1"}),"instanceName":"1"}),"instanceName":"1"});
            var Q163;
            Q163=makeQuery(id+"F9.opPattern","COPY",BODY,{"derivedFrom":makeQuery(id+"F8.opPattern","COPY",BODY,{"derivedFrom":makeQuery(id+"F6.opPattern","COPY",BODY,{"derivedFrom":makeQuery(id+"F5.opPattern","COPY",BODY,{"derivedFrom":makeQuery(id+"F2.opPattern","COPY",BODY,{"derivedFrom":makeQuery(id+"F1.opRevolve","SWEPT_BODY",BODY,{"disambiguationData":[OSD([sQuery(id+"F0.wireOp",EDGE,"E1")])]}),"instanceName":"1"}),"instanceName":"1"}),"instanceName":"1"}),"instanceName":"1"}),"instanceName":"1"});
            var Q164;
            Q164=makeQuery(id+"F9.opPattern","COPY",BODY,{"derivedFrom":makeQuery(id+"F8.opPattern","COPY",BODY,{"derivedFrom":makeQuery(id+"F6.opPattern","COPY",BODY,{"derivedFrom":makeQuery(id+"F5.opPattern","COPY",BODY,{"derivedFrom":makeQuery(id+"F3.opPattern","COPY",BODY,{"derivedFrom":makeQuery(id+"F2.opPattern","COPY",BODY,{"derivedFrom":makeQuery(id+"F1.opRevolve","SWEPT_BODY",BODY,{"disambiguationData":[OSD([sQuery(id+"F0.wireOp",EDGE,"E1")])]}),"instanceName":"1"}),"instanceName":"1"}),"instanceName":"1"}),"instanceName":"1"}),"instanceName":"1"}),"instanceName":"1"});
            var Q165;
            Q165=makeQuery(id+"F9.opPattern","COPY",BODY,{"derivedFrom":makeQuery(id+"F8.opPattern","COPY",BODY,{"derivedFrom":makeQuery(id+"F6.opPattern","COPY",BODY,{"derivedFrom":makeQuery(id+"F5.opPattern","COPY",BODY,{"derivedFrom":makeQuery(id+"F4.opPattern","COPY",BODY,{"derivedFrom":makeQuery(id+"F1.opRevolve","SWEPT_BODY",BODY,{"disambiguationData":[OSD([sQuery(id+"F0.wireOp",EDGE,"E1")])]}),"instanceName":"1"}),"instanceName":"1"}),"instanceName":"1"}),"instanceName":"1"}),"instanceName":"1"});
            var Q166;
            Q166=makeQuery(id+"F9.opPattern","COPY",BODY,{"derivedFrom":makeQuery(id+"F8.opPattern","COPY",BODY,{"derivedFrom":makeQuery(id+"F6.opPattern","COPY",BODY,{"derivedFrom":makeQuery(id+"F5.opPattern","COPY",BODY,{"derivedFrom":makeQuery(id+"F4.opPattern","COPY",BODY,{"derivedFrom":makeQuery(id+"F2.opPattern","COPY",BODY,{"derivedFrom":makeQuery(id+"F1.opRevolve","SWEPT_BODY",BODY,{"disambiguationData":[OSD([sQuery(id+"F0.wireOp",EDGE,"E1")])]}),"instanceName":"1"}),"instanceName":"1"}),"instanceName":"1"}),"instanceName":"1"}),"instanceName":"1"}),"instanceName":"1"});
            var Q167;
            Q167=makeQuery(id+"F9.opPattern","COPY",BODY,{"derivedFrom":makeQuery(id+"F8.opPattern","COPY",BODY,{"derivedFrom":makeQuery(id+"F6.opPattern","COPY",BODY,{"derivedFrom":makeQuery(id+"F5.opPattern","COPY",BODY,{"derivedFrom":makeQuery(id+"F4.opPattern","COPY",BODY,{"derivedFrom":makeQuery(id+"F3.opPattern","COPY",BODY,{"derivedFrom":makeQuery(id+"F2.opPattern","COPY",BODY,{"derivedFrom":makeQuery(id+"F1.opRevolve","SWEPT_BODY",BODY,{"disambiguationData":[OSD([sQuery(id+"F0.wireOp",EDGE,"E1")])]}),"instanceName":"1"}),"instanceName":"1"}),"instanceName":"1"}),"instanceName":"1"}),"instanceName":"1"}),"instanceName":"1"}),"instanceName":"1"});
            var Q168;
            Q168=makeQuery(id+"F9.opPattern","COPY",BODY,{"derivedFrom":makeQuery(id+"F8.opPattern","COPY",BODY,{"derivedFrom":makeQuery(id+"F7.opPattern","COPY",BODY,{"derivedFrom":makeQuery(id+"F1.opRevolve","SWEPT_BODY",BODY,{"disambiguationData":[OSD([sQuery(id+"F0.wireOp",EDGE,"E1")])]}),"instanceName":"1"}),"instanceName":"1"}),"instanceName":"1"});
            var Q169;
            Q169=makeQuery(id+"F9.opPattern","COPY",BODY,{"derivedFrom":makeQuery(id+"F8.opPattern","COPY",BODY,{"derivedFrom":makeQuery(id+"F7.opPattern","COPY",BODY,{"derivedFrom":makeQuery(id+"F2.opPattern","COPY",BODY,{"derivedFrom":makeQuery(id+"F1.opRevolve","SWEPT_BODY",BODY,{"disambiguationData":[OSD([sQuery(id+"F0.wireOp",EDGE,"E1")])]}),"instanceName":"1"}),"instanceName":"1"}),"instanceName":"1"}),"instanceName":"1"});
            var Q170;
            Q170=makeQuery(id+"F9.opPattern","COPY",BODY,{"derivedFrom":makeQuery(id+"F8.opPattern","COPY",BODY,{"derivedFrom":makeQuery(id+"F7.opPattern","COPY",BODY,{"derivedFrom":makeQuery(id+"F3.opPattern","COPY",BODY,{"derivedFrom":makeQuery(id+"F2.opPattern","COPY",BODY,{"derivedFrom":makeQuery(id+"F1.opRevolve","SWEPT_BODY",BODY,{"disambiguationData":[OSD([sQuery(id+"F0.wireOp",EDGE,"E1")])]}),"instanceName":"1"}),"instanceName":"1"}),"instanceName":"1"}),"instanceName":"1"}),"instanceName":"1"});
            var Q171;
            Q171=makeQuery(id+"F9.opPattern","COPY",BODY,{"derivedFrom":makeQuery(id+"F8.opPattern","COPY",BODY,{"derivedFrom":makeQuery(id+"F7.opPattern","COPY",BODY,{"derivedFrom":makeQuery(id+"F4.opPattern","COPY",BODY,{"derivedFrom":makeQuery(id+"F1.opRevolve","SWEPT_BODY",BODY,{"disambiguationData":[OSD([sQuery(id+"F0.wireOp",EDGE,"E1")])]}),"instanceName":"1"}),"instanceName":"1"}),"instanceName":"1"}),"instanceName":"1"});
            var Q172;
            Q172=makeQuery(id+"F9.opPattern","COPY",BODY,{"derivedFrom":makeQuery(id+"F8.opPattern","COPY",BODY,{"derivedFrom":makeQuery(id+"F7.opPattern","COPY",BODY,{"derivedFrom":makeQuery(id+"F4.opPattern","COPY",BODY,{"derivedFrom":makeQuery(id+"F2.opPattern","COPY",BODY,{"derivedFrom":makeQuery(id+"F1.opRevolve","SWEPT_BODY",BODY,{"disambiguationData":[OSD([sQuery(id+"F0.wireOp",EDGE,"E1")])]}),"instanceName":"1"}),"instanceName":"1"}),"instanceName":"1"}),"instanceName":"1"}),"instanceName":"1"});
            var Q173;
            Q173=makeQuery(id+"F9.opPattern","COPY",BODY,{"derivedFrom":makeQuery(id+"F8.opPattern","COPY",BODY,{"derivedFrom":makeQuery(id+"F7.opPattern","COPY",BODY,{"derivedFrom":makeQuery(id+"F4.opPattern","COPY",BODY,{"derivedFrom":makeQuery(id+"F3.opPattern","COPY",BODY,{"derivedFrom":makeQuery(id+"F2.opPattern","COPY",BODY,{"derivedFrom":makeQuery(id+"F1.opRevolve","SWEPT_BODY",BODY,{"disambiguationData":[OSD([sQuery(id+"F0.wireOp",EDGE,"E1")])]}),"instanceName":"1"}),"instanceName":"1"}),"instanceName":"1"}),"instanceName":"1"}),"instanceName":"1"}),"instanceName":"1"});
            var Q174;
            Q174=makeQuery(id+"F9.opPattern","COPY",BODY,{"derivedFrom":makeQuery(id+"F8.opPattern","COPY",BODY,{"derivedFrom":makeQuery(id+"F7.opPattern","COPY",BODY,{"derivedFrom":makeQuery(id+"F5.opPattern","COPY",BODY,{"derivedFrom":makeQuery(id+"F1.opRevolve","SWEPT_BODY",BODY,{"disambiguationData":[OSD([sQuery(id+"F0.wireOp",EDGE,"E1")])]}),"instanceName":"1"}),"instanceName":"1"}),"instanceName":"1"}),"instanceName":"1"});
            var Q175;
            Q175=makeQuery(id+"F9.opPattern","COPY",BODY,{"derivedFrom":makeQuery(id+"F8.opPattern","COPY",BODY,{"derivedFrom":makeQuery(id+"F7.opPattern","COPY",BODY,{"derivedFrom":makeQuery(id+"F5.opPattern","COPY",BODY,{"derivedFrom":makeQuery(id+"F2.opPattern","COPY",BODY,{"derivedFrom":makeQuery(id+"F1.opRevolve","SWEPT_BODY",BODY,{"disambiguationData":[OSD([sQuery(id+"F0.wireOp",EDGE,"E1")])]}),"instanceName":"1"}),"instanceName":"1"}),"instanceName":"1"}),"instanceName":"1"}),"instanceName":"1"});
            var Q176;
            Q176=makeQuery(id+"F9.opPattern","COPY",BODY,{"derivedFrom":makeQuery(id+"F8.opPattern","COPY",BODY,{"derivedFrom":makeQuery(id+"F7.opPattern","COPY",BODY,{"derivedFrom":makeQuery(id+"F5.opPattern","COPY",BODY,{"derivedFrom":makeQuery(id+"F3.opPattern","COPY",BODY,{"derivedFrom":makeQuery(id+"F2.opPattern","COPY",BODY,{"derivedFrom":makeQuery(id+"F1.opRevolve","SWEPT_BODY",BODY,{"disambiguationData":[OSD([sQuery(id+"F0.wireOp",EDGE,"E1")])]}),"instanceName":"1"}),"instanceName":"1"}),"instanceName":"1"}),"instanceName":"1"}),"instanceName":"1"}),"instanceName":"1"});
            var Q177;
            Q177=makeQuery(id+"F9.opPattern","COPY",BODY,{"derivedFrom":makeQuery(id+"F8.opPattern","COPY",BODY,{"derivedFrom":makeQuery(id+"F7.opPattern","COPY",BODY,{"derivedFrom":makeQuery(id+"F5.opPattern","COPY",BODY,{"derivedFrom":makeQuery(id+"F4.opPattern","COPY",BODY,{"derivedFrom":makeQuery(id+"F1.opRevolve","SWEPT_BODY",BODY,{"disambiguationData":[OSD([sQuery(id+"F0.wireOp",EDGE,"E1")])]}),"instanceName":"1"}),"instanceName":"1"}),"instanceName":"1"}),"instanceName":"1"}),"instanceName":"1"});
            var Q178;
            Q178=makeQuery(id+"F9.opPattern","COPY",BODY,{"derivedFrom":makeQuery(id+"F8.opPattern","COPY",BODY,{"derivedFrom":makeQuery(id+"F7.opPattern","COPY",BODY,{"derivedFrom":makeQuery(id+"F5.opPattern","COPY",BODY,{"derivedFrom":makeQuery(id+"F4.opPattern","COPY",BODY,{"derivedFrom":makeQuery(id+"F2.opPattern","COPY",BODY,{"derivedFrom":makeQuery(id+"F1.opRevolve","SWEPT_BODY",BODY,{"disambiguationData":[OSD([sQuery(id+"F0.wireOp",EDGE,"E1")])]}),"instanceName":"1"}),"instanceName":"1"}),"instanceName":"1"}),"instanceName":"1"}),"instanceName":"1"}),"instanceName":"1"});
            var Q179;
            Q179=makeQuery(id+"F9.opPattern","COPY",BODY,{"derivedFrom":makeQuery(id+"F8.opPattern","COPY",BODY,{"derivedFrom":makeQuery(id+"F7.opPattern","COPY",BODY,{"derivedFrom":makeQuery(id+"F5.opPattern","COPY",BODY,{"derivedFrom":makeQuery(id+"F4.opPattern","COPY",BODY,{"derivedFrom":makeQuery(id+"F3.opPattern","COPY",BODY,{"derivedFrom":makeQuery(id+"F2.opPattern","COPY",BODY,{"derivedFrom":makeQuery(id+"F1.opRevolve","SWEPT_BODY",BODY,{"disambiguationData":[OSD([sQuery(id+"F0.wireOp",EDGE,"E1")])]}),"instanceName":"1"}),"instanceName":"1"}),"instanceName":"1"}),"instanceName":"1"}),"instanceName":"1"}),"instanceName":"1"}),"instanceName":"1"});
            var Q180;
            Q180=makeQuery(id+"F9.opPattern","COPY",BODY,{"derivedFrom":makeQuery(id+"F8.opPattern","COPY",BODY,{"derivedFrom":makeQuery(id+"F7.opPattern","COPY",BODY,{"derivedFrom":makeQuery(id+"F6.opPattern","COPY",BODY,{"derivedFrom":makeQuery(id+"F1.opRevolve","SWEPT_BODY",BODY,{"disambiguationData":[OSD([sQuery(id+"F0.wireOp",EDGE,"E1")])]}),"instanceName":"1"}),"instanceName":"1"}),"instanceName":"1"}),"instanceName":"1"});
            var Q181;
            Q181=makeQuery(id+"F9.opPattern","COPY",BODY,{"derivedFrom":makeQuery(id+"F8.opPattern","COPY",BODY,{"derivedFrom":makeQuery(id+"F7.opPattern","COPY",BODY,{"derivedFrom":makeQuery(id+"F6.opPattern","COPY",BODY,{"derivedFrom":makeQuery(id+"F2.opPattern","COPY",BODY,{"derivedFrom":makeQuery(id+"F1.opRevolve","SWEPT_BODY",BODY,{"disambiguationData":[OSD([sQuery(id+"F0.wireOp",EDGE,"E1")])]}),"instanceName":"1"}),"instanceName":"1"}),"instanceName":"1"}),"instanceName":"1"}),"instanceName":"1"});
            var Q182;
            Q182=makeQuery(id+"F9.opPattern","COPY",BODY,{"derivedFrom":makeQuery(id+"F8.opPattern","COPY",BODY,{"derivedFrom":makeQuery(id+"F7.opPattern","COPY",BODY,{"derivedFrom":makeQuery(id+"F6.opPattern","COPY",BODY,{"derivedFrom":makeQuery(id+"F3.opPattern","COPY",BODY,{"derivedFrom":makeQuery(id+"F2.opPattern","COPY",BODY,{"derivedFrom":makeQuery(id+"F1.opRevolve","SWEPT_BODY",BODY,{"disambiguationData":[OSD([sQuery(id+"F0.wireOp",EDGE,"E1")])]}),"instanceName":"1"}),"instanceName":"1"}),"instanceName":"1"}),"instanceName":"1"}),"instanceName":"1"}),"instanceName":"1"});
            var Q183;
            Q183=makeQuery(id+"F9.opPattern","COPY",BODY,{"derivedFrom":makeQuery(id+"F8.opPattern","COPY",BODY,{"derivedFrom":makeQuery(id+"F7.opPattern","COPY",BODY,{"derivedFrom":makeQuery(id+"F6.opPattern","COPY",BODY,{"derivedFrom":makeQuery(id+"F4.opPattern","COPY",BODY,{"derivedFrom":makeQuery(id+"F1.opRevolve","SWEPT_BODY",BODY,{"disambiguationData":[OSD([sQuery(id+"F0.wireOp",EDGE,"E1")])]}),"instanceName":"1"}),"instanceName":"1"}),"instanceName":"1"}),"instanceName":"1"}),"instanceName":"1"});
            var Q184;
            Q184=makeQuery(id+"F9.opPattern","COPY",BODY,{"derivedFrom":makeQuery(id+"F8.opPattern","COPY",BODY,{"derivedFrom":makeQuery(id+"F7.opPattern","COPY",BODY,{"derivedFrom":makeQuery(id+"F6.opPattern","COPY",BODY,{"derivedFrom":makeQuery(id+"F4.opPattern","COPY",BODY,{"derivedFrom":makeQuery(id+"F2.opPattern","COPY",BODY,{"derivedFrom":makeQuery(id+"F1.opRevolve","SWEPT_BODY",BODY,{"disambiguationData":[OSD([sQuery(id+"F0.wireOp",EDGE,"E1")])]}),"instanceName":"1"}),"instanceName":"1"}),"instanceName":"1"}),"instanceName":"1"}),"instanceName":"1"}),"instanceName":"1"});
            var Q185;
            Q185=makeQuery(id+"F9.opPattern","COPY",BODY,{"derivedFrom":makeQuery(id+"F8.opPattern","COPY",BODY,{"derivedFrom":makeQuery(id+"F7.opPattern","COPY",BODY,{"derivedFrom":makeQuery(id+"F6.opPattern","COPY",BODY,{"derivedFrom":makeQuery(id+"F4.opPattern","COPY",BODY,{"derivedFrom":makeQuery(id+"F3.opPattern","COPY",BODY,{"derivedFrom":makeQuery(id+"F2.opPattern","COPY",BODY,{"derivedFrom":makeQuery(id+"F1.opRevolve","SWEPT_BODY",BODY,{"disambiguationData":[OSD([sQuery(id+"F0.wireOp",EDGE,"E1")])]}),"instanceName":"1"}),"instanceName":"1"}),"instanceName":"1"}),"instanceName":"1"}),"instanceName":"1"}),"instanceName":"1"}),"instanceName":"1"});
            var Q186;
            Q186=makeQuery(id+"F9.opPattern","COPY",BODY,{"derivedFrom":makeQuery(id+"F8.opPattern","COPY",BODY,{"derivedFrom":makeQuery(id+"F7.opPattern","COPY",BODY,{"derivedFrom":makeQuery(id+"F6.opPattern","COPY",BODY,{"derivedFrom":makeQuery(id+"F5.opPattern","COPY",BODY,{"derivedFrom":makeQuery(id+"F1.opRevolve","SWEPT_BODY",BODY,{"disambiguationData":[OSD([sQuery(id+"F0.wireOp",EDGE,"E1")])]}),"instanceName":"1"}),"instanceName":"1"}),"instanceName":"1"}),"instanceName":"1"}),"instanceName":"1"});
            var Q187;
            Q187=makeQuery(id+"F9.opPattern","COPY",BODY,{"derivedFrom":makeQuery(id+"F8.opPattern","COPY",BODY,{"derivedFrom":makeQuery(id+"F7.opPattern","COPY",BODY,{"derivedFrom":makeQuery(id+"F6.opPattern","COPY",BODY,{"derivedFrom":makeQuery(id+"F5.opPattern","COPY",BODY,{"derivedFrom":makeQuery(id+"F2.opPattern","COPY",BODY,{"derivedFrom":makeQuery(id+"F1.opRevolve","SWEPT_BODY",BODY,{"disambiguationData":[OSD([sQuery(id+"F0.wireOp",EDGE,"E1")])]}),"instanceName":"1"}),"instanceName":"1"}),"instanceName":"1"}),"instanceName":"1"}),"instanceName":"1"}),"instanceName":"1"});
            var Q188;
            Q188=makeQuery(id+"F9.opPattern","COPY",BODY,{"derivedFrom":makeQuery(id+"F8.opPattern","COPY",BODY,{"derivedFrom":makeQuery(id+"F7.opPattern","COPY",BODY,{"derivedFrom":makeQuery(id+"F6.opPattern","COPY",BODY,{"derivedFrom":makeQuery(id+"F5.opPattern","COPY",BODY,{"derivedFrom":makeQuery(id+"F3.opPattern","COPY",BODY,{"derivedFrom":makeQuery(id+"F2.opPattern","COPY",BODY,{"derivedFrom":makeQuery(id+"F1.opRevolve","SWEPT_BODY",BODY,{"disambiguationData":[OSD([sQuery(id+"F0.wireOp",EDGE,"E1")])]}),"instanceName":"1"}),"instanceName":"1"}),"instanceName":"1"}),"instanceName":"1"}),"instanceName":"1"}),"instanceName":"1"}),"instanceName":"1"});
            var Q189;
            Q189=makeQuery(id+"F9.opPattern","COPY",BODY,{"derivedFrom":makeQuery(id+"F8.opPattern","COPY",BODY,{"derivedFrom":makeQuery(id+"F7.opPattern","COPY",BODY,{"derivedFrom":makeQuery(id+"F6.opPattern","COPY",BODY,{"derivedFrom":makeQuery(id+"F5.opPattern","COPY",BODY,{"derivedFrom":makeQuery(id+"F4.opPattern","COPY",BODY,{"derivedFrom":makeQuery(id+"F1.opRevolve","SWEPT_BODY",BODY,{"disambiguationData":[OSD([sQuery(id+"F0.wireOp",EDGE,"E1")])]}),"instanceName":"1"}),"instanceName":"1"}),"instanceName":"1"}),"instanceName":"1"}),"instanceName":"1"}),"instanceName":"1"});
            var Q190;
            Q190=makeQuery(id+"F9.opPattern","COPY",BODY,{"derivedFrom":makeQuery(id+"F8.opPattern","COPY",BODY,{"derivedFrom":makeQuery(id+"F7.opPattern","COPY",BODY,{"derivedFrom":makeQuery(id+"F6.opPattern","COPY",BODY,{"derivedFrom":makeQuery(id+"F5.opPattern","COPY",BODY,{"derivedFrom":makeQuery(id+"F4.opPattern","COPY",BODY,{"derivedFrom":makeQuery(id+"F2.opPattern","COPY",BODY,{"derivedFrom":makeQuery(id+"F1.opRevolve","SWEPT_BODY",BODY,{"disambiguationData":[OSD([sQuery(id+"F0.wireOp",EDGE,"E1")])]}),"instanceName":"1"}),"instanceName":"1"}),"instanceName":"1"}),"instanceName":"1"}),"instanceName":"1"}),"instanceName":"1"}),"instanceName":"1"});
            var Q191;
            Q191=makeQuery(id+"F9.opPattern","COPY",BODY,{"derivedFrom":makeQuery(id+"F8.opPattern","COPY",BODY,{"derivedFrom":makeQuery(id+"F7.opPattern","COPY",BODY,{"derivedFrom":makeQuery(id+"F6.opPattern","COPY",BODY,{"derivedFrom":makeQuery(id+"F5.opPattern","COPY",BODY,{"derivedFrom":makeQuery(id+"F4.opPattern","COPY",BODY,{"derivedFrom":makeQuery(id+"F3.opPattern","COPY",BODY,{"derivedFrom":makeQuery(id+"F2.opPattern","COPY",BODY,{"derivedFrom":makeQuery(id+"F1.opRevolve","SWEPT_BODY",BODY,{"disambiguationData":[OSD([sQuery(id+"F0.wireOp",EDGE,"E1")])]}),"instanceName":"1"}),"instanceName":"1"}),"instanceName":"1"}),"instanceName":"1"}),"instanceName":"1"}),"instanceName":"1"}),"instanceName":"1"}),"instanceName":"1"});
            var Q192;
            Q192=makeQuery(id+"F10.opPattern","COPY",BODY,{"derivedFrom":makeQuery(id+"F1.opRevolve","SWEPT_BODY",BODY,{"disambiguationData":[OSD([sQuery(id+"F0.wireOp",EDGE,"E1")])]}),"instanceName":"1"});
            var Q193;
            Q193=makeQuery(id+"F10.opPattern","COPY",BODY,{"derivedFrom":makeQuery(id+"F2.opPattern","COPY",BODY,{"derivedFrom":makeQuery(id+"F1.opRevolve","SWEPT_BODY",BODY,{"disambiguationData":[OSD([sQuery(id+"F0.wireOp",EDGE,"E1")])]}),"instanceName":"1"}),"instanceName":"1"});
            var Q194;
            Q194=makeQuery(id+"F10.opPattern","COPY",BODY,{"derivedFrom":makeQuery(id+"F3.opPattern","COPY",BODY,{"derivedFrom":makeQuery(id+"F2.opPattern","COPY",BODY,{"derivedFrom":makeQuery(id+"F1.opRevolve","SWEPT_BODY",BODY,{"disambiguationData":[OSD([sQuery(id+"F0.wireOp",EDGE,"E1")])]}),"instanceName":"1"}),"instanceName":"1"}),"instanceName":"1"});
            var Q195;
            Q195=makeQuery(id+"F10.opPattern","COPY",BODY,{"derivedFrom":makeQuery(id+"F4.opPattern","COPY",BODY,{"derivedFrom":makeQuery(id+"F1.opRevolve","SWEPT_BODY",BODY,{"disambiguationData":[OSD([sQuery(id+"F0.wireOp",EDGE,"E1")])]}),"instanceName":"1"}),"instanceName":"1"});
            var Q196;
            Q196=makeQuery(id+"F10.opPattern","COPY",BODY,{"derivedFrom":makeQuery(id+"F4.opPattern","COPY",BODY,{"derivedFrom":makeQuery(id+"F2.opPattern","COPY",BODY,{"derivedFrom":makeQuery(id+"F1.opRevolve","SWEPT_BODY",BODY,{"disambiguationData":[OSD([sQuery(id+"F0.wireOp",EDGE,"E1")])]}),"instanceName":"1"}),"instanceName":"1"}),"instanceName":"1"});
            var Q197;
            Q197=makeQuery(id+"F10.opPattern","COPY",BODY,{"derivedFrom":makeQuery(id+"F4.opPattern","COPY",BODY,{"derivedFrom":makeQuery(id+"F3.opPattern","COPY",BODY,{"derivedFrom":makeQuery(id+"F2.opPattern","COPY",BODY,{"derivedFrom":makeQuery(id+"F1.opRevolve","SWEPT_BODY",BODY,{"disambiguationData":[OSD([sQuery(id+"F0.wireOp",EDGE,"E1")])]}),"instanceName":"1"}),"instanceName":"1"}),"instanceName":"1"}),"instanceName":"1"});
            var Q198;
            Q198=makeQuery(id+"F10.opPattern","COPY",BODY,{"derivedFrom":makeQuery(id+"F5.opPattern","COPY",BODY,{"derivedFrom":makeQuery(id+"F1.opRevolve","SWEPT_BODY",BODY,{"disambiguationData":[OSD([sQuery(id+"F0.wireOp",EDGE,"E1")])]}),"instanceName":"1"}),"instanceName":"1"});
            var Q199;
            Q199=makeQuery(id+"F10.opPattern","COPY",BODY,{"derivedFrom":makeQuery(id+"F5.opPattern","COPY",BODY,{"derivedFrom":makeQuery(id+"F2.opPattern","COPY",BODY,{"derivedFrom":makeQuery(id+"F1.opRevolve","SWEPT_BODY",BODY,{"disambiguationData":[OSD([sQuery(id+"F0.wireOp",EDGE,"E1")])]}),"instanceName":"1"}),"instanceName":"1"}),"instanceName":"1"});
            var Q200;
            Q200=makeQuery(id+"F10.opPattern","COPY",BODY,{"derivedFrom":makeQuery(id+"F5.opPattern","COPY",BODY,{"derivedFrom":makeQuery(id+"F3.opPattern","COPY",BODY,{"derivedFrom":makeQuery(id+"F2.opPattern","COPY",BODY,{"derivedFrom":makeQuery(id+"F1.opRevolve","SWEPT_BODY",BODY,{"disambiguationData":[OSD([sQuery(id+"F0.wireOp",EDGE,"E1")])]}),"instanceName":"1"}),"instanceName":"1"}),"instanceName":"1"}),"instanceName":"1"});
            var Q201;
            Q201=makeQuery(id+"F10.opPattern","COPY",BODY,{"derivedFrom":makeQuery(id+"F5.opPattern","COPY",BODY,{"derivedFrom":makeQuery(id+"F4.opPattern","COPY",BODY,{"derivedFrom":makeQuery(id+"F1.opRevolve","SWEPT_BODY",BODY,{"disambiguationData":[OSD([sQuery(id+"F0.wireOp",EDGE,"E1")])]}),"instanceName":"1"}),"instanceName":"1"}),"instanceName":"1"});
            var Q202;
            Q202=makeQuery(id+"F10.opPattern","COPY",BODY,{"derivedFrom":makeQuery(id+"F5.opPattern","COPY",BODY,{"derivedFrom":makeQuery(id+"F4.opPattern","COPY",BODY,{"derivedFrom":makeQuery(id+"F2.opPattern","COPY",BODY,{"derivedFrom":makeQuery(id+"F1.opRevolve","SWEPT_BODY",BODY,{"disambiguationData":[OSD([sQuery(id+"F0.wireOp",EDGE,"E1")])]}),"instanceName":"1"}),"instanceName":"1"}),"instanceName":"1"}),"instanceName":"1"});
            var Q203;
            Q203=makeQuery(id+"F10.opPattern","COPY",BODY,{"derivedFrom":makeQuery(id+"F5.opPattern","COPY",BODY,{"derivedFrom":makeQuery(id+"F4.opPattern","COPY",BODY,{"derivedFrom":makeQuery(id+"F3.opPattern","COPY",BODY,{"derivedFrom":makeQuery(id+"F2.opPattern","COPY",BODY,{"derivedFrom":makeQuery(id+"F1.opRevolve","SWEPT_BODY",BODY,{"disambiguationData":[OSD([sQuery(id+"F0.wireOp",EDGE,"E1")])]}),"instanceName":"1"}),"instanceName":"1"}),"instanceName":"1"}),"instanceName":"1"}),"instanceName":"1"});
            var Q204;
            Q204=makeQuery(id+"F10.opPattern","COPY",BODY,{"derivedFrom":makeQuery(id+"F6.opPattern","COPY",BODY,{"derivedFrom":makeQuery(id+"F1.opRevolve","SWEPT_BODY",BODY,{"disambiguationData":[OSD([sQuery(id+"F0.wireOp",EDGE,"E1")])]}),"instanceName":"1"}),"instanceName":"1"});
            var Q205;
            Q205=makeQuery(id+"F10.opPattern","COPY",BODY,{"derivedFrom":makeQuery(id+"F6.opPattern","COPY",BODY,{"derivedFrom":makeQuery(id+"F2.opPattern","COPY",BODY,{"derivedFrom":makeQuery(id+"F1.opRevolve","SWEPT_BODY",BODY,{"disambiguationData":[OSD([sQuery(id+"F0.wireOp",EDGE,"E1")])]}),"instanceName":"1"}),"instanceName":"1"}),"instanceName":"1"});
            var Q206;
            Q206=makeQuery(id+"F10.opPattern","COPY",BODY,{"derivedFrom":makeQuery(id+"F6.opPattern","COPY",BODY,{"derivedFrom":makeQuery(id+"F3.opPattern","COPY",BODY,{"derivedFrom":makeQuery(id+"F2.opPattern","COPY",BODY,{"derivedFrom":makeQuery(id+"F1.opRevolve","SWEPT_BODY",BODY,{"disambiguationData":[OSD([sQuery(id+"F0.wireOp",EDGE,"E1")])]}),"instanceName":"1"}),"instanceName":"1"}),"instanceName":"1"}),"instanceName":"1"});
            var Q207;
            Q207=makeQuery(id+"F10.opPattern","COPY",BODY,{"derivedFrom":makeQuery(id+"F6.opPattern","COPY",BODY,{"derivedFrom":makeQuery(id+"F4.opPattern","COPY",BODY,{"derivedFrom":makeQuery(id+"F1.opRevolve","SWEPT_BODY",BODY,{"disambiguationData":[OSD([sQuery(id+"F0.wireOp",EDGE,"E1")])]}),"instanceName":"1"}),"instanceName":"1"}),"instanceName":"1"});
            var Q208;
            Q208=makeQuery(id+"F10.opPattern","COPY",BODY,{"derivedFrom":makeQuery(id+"F6.opPattern","COPY",BODY,{"derivedFrom":makeQuery(id+"F4.opPattern","COPY",BODY,{"derivedFrom":makeQuery(id+"F2.opPattern","COPY",BODY,{"derivedFrom":makeQuery(id+"F1.opRevolve","SWEPT_BODY",BODY,{"disambiguationData":[OSD([sQuery(id+"F0.wireOp",EDGE,"E1")])]}),"instanceName":"1"}),"instanceName":"1"}),"instanceName":"1"}),"instanceName":"1"});
            var Q209;
            Q209=makeQuery(id+"F10.opPattern","COPY",BODY,{"derivedFrom":makeQuery(id+"F6.opPattern","COPY",BODY,{"derivedFrom":makeQuery(id+"F4.opPattern","COPY",BODY,{"derivedFrom":makeQuery(id+"F3.opPattern","COPY",BODY,{"derivedFrom":makeQuery(id+"F2.opPattern","COPY",BODY,{"derivedFrom":makeQuery(id+"F1.opRevolve","SWEPT_BODY",BODY,{"disambiguationData":[OSD([sQuery(id+"F0.wireOp",EDGE,"E1")])]}),"instanceName":"1"}),"instanceName":"1"}),"instanceName":"1"}),"instanceName":"1"}),"instanceName":"1"});
            var Q210;
            Q210=makeQuery(id+"F10.opPattern","COPY",BODY,{"derivedFrom":makeQuery(id+"F6.opPattern","COPY",BODY,{"derivedFrom":makeQuery(id+"F5.opPattern","COPY",BODY,{"derivedFrom":makeQuery(id+"F1.opRevolve","SWEPT_BODY",BODY,{"disambiguationData":[OSD([sQuery(id+"F0.wireOp",EDGE,"E1")])]}),"instanceName":"1"}),"instanceName":"1"}),"instanceName":"1"});
            var Q211;
            Q211=makeQuery(id+"F10.opPattern","COPY",BODY,{"derivedFrom":makeQuery(id+"F6.opPattern","COPY",BODY,{"derivedFrom":makeQuery(id+"F5.opPattern","COPY",BODY,{"derivedFrom":makeQuery(id+"F2.opPattern","COPY",BODY,{"derivedFrom":makeQuery(id+"F1.opRevolve","SWEPT_BODY",BODY,{"disambiguationData":[OSD([sQuery(id+"F0.wireOp",EDGE,"E1")])]}),"instanceName":"1"}),"instanceName":"1"}),"instanceName":"1"}),"instanceName":"1"});
            var Q212;
            Q212=makeQuery(id+"F10.opPattern","COPY",BODY,{"derivedFrom":makeQuery(id+"F6.opPattern","COPY",BODY,{"derivedFrom":makeQuery(id+"F5.opPattern","COPY",BODY,{"derivedFrom":makeQuery(id+"F3.opPattern","COPY",BODY,{"derivedFrom":makeQuery(id+"F2.opPattern","COPY",BODY,{"derivedFrom":makeQuery(id+"F1.opRevolve","SWEPT_BODY",BODY,{"disambiguationData":[OSD([sQuery(id+"F0.wireOp",EDGE,"E1")])]}),"instanceName":"1"}),"instanceName":"1"}),"instanceName":"1"}),"instanceName":"1"}),"instanceName":"1"});
            var Q213;
            Q213=makeQuery(id+"F10.opPattern","COPY",BODY,{"derivedFrom":makeQuery(id+"F6.opPattern","COPY",BODY,{"derivedFrom":makeQuery(id+"F5.opPattern","COPY",BODY,{"derivedFrom":makeQuery(id+"F4.opPattern","COPY",BODY,{"derivedFrom":makeQuery(id+"F1.opRevolve","SWEPT_BODY",BODY,{"disambiguationData":[OSD([sQuery(id+"F0.wireOp",EDGE,"E1")])]}),"instanceName":"1"}),"instanceName":"1"}),"instanceName":"1"}),"instanceName":"1"});
            var Q214;
            Q214=makeQuery(id+"F10.opPattern","COPY",BODY,{"derivedFrom":makeQuery(id+"F6.opPattern","COPY",BODY,{"derivedFrom":makeQuery(id+"F5.opPattern","COPY",BODY,{"derivedFrom":makeQuery(id+"F4.opPattern","COPY",BODY,{"derivedFrom":makeQuery(id+"F2.opPattern","COPY",BODY,{"derivedFrom":makeQuery(id+"F1.opRevolve","SWEPT_BODY",BODY,{"disambiguationData":[OSD([sQuery(id+"F0.wireOp",EDGE,"E1")])]}),"instanceName":"1"}),"instanceName":"1"}),"instanceName":"1"}),"instanceName":"1"}),"instanceName":"1"});
            var Q215;
            Q215=makeQuery(id+"F10.opPattern","COPY",BODY,{"derivedFrom":makeQuery(id+"F6.opPattern","COPY",BODY,{"derivedFrom":makeQuery(id+"F5.opPattern","COPY",BODY,{"derivedFrom":makeQuery(id+"F4.opPattern","COPY",BODY,{"derivedFrom":makeQuery(id+"F3.opPattern","COPY",BODY,{"derivedFrom":makeQuery(id+"F2.opPattern","COPY",BODY,{"derivedFrom":makeQuery(id+"F1.opRevolve","SWEPT_BODY",BODY,{"disambiguationData":[OSD([sQuery(id+"F0.wireOp",EDGE,"E1")])]}),"instanceName":"1"}),"instanceName":"1"}),"instanceName":"1"}),"instanceName":"1"}),"instanceName":"1"}),"instanceName":"1"});
            var Q216;
            Q216=makeQuery(id+"F10.opPattern","COPY",BODY,{"derivedFrom":makeQuery(id+"F7.opPattern","COPY",BODY,{"derivedFrom":makeQuery(id+"F1.opRevolve","SWEPT_BODY",BODY,{"disambiguationData":[OSD([sQuery(id+"F0.wireOp",EDGE,"E1")])]}),"instanceName":"1"}),"instanceName":"1"});
            var Q217;
            Q217=makeQuery(id+"F10.opPattern","COPY",BODY,{"derivedFrom":makeQuery(id+"F7.opPattern","COPY",BODY,{"derivedFrom":makeQuery(id+"F2.opPattern","COPY",BODY,{"derivedFrom":makeQuery(id+"F1.opRevolve","SWEPT_BODY",BODY,{"disambiguationData":[OSD([sQuery(id+"F0.wireOp",EDGE,"E1")])]}),"instanceName":"1"}),"instanceName":"1"}),"instanceName":"1"});
            var Q218;
            Q218=makeQuery(id+"F10.opPattern","COPY",BODY,{"derivedFrom":makeQuery(id+"F7.opPattern","COPY",BODY,{"derivedFrom":makeQuery(id+"F3.opPattern","COPY",BODY,{"derivedFrom":makeQuery(id+"F2.opPattern","COPY",BODY,{"derivedFrom":makeQuery(id+"F1.opRevolve","SWEPT_BODY",BODY,{"disambiguationData":[OSD([sQuery(id+"F0.wireOp",EDGE,"E1")])]}),"instanceName":"1"}),"instanceName":"1"}),"instanceName":"1"}),"instanceName":"1"});
            var Q219;
            Q219=makeQuery(id+"F10.opPattern","COPY",BODY,{"derivedFrom":makeQuery(id+"F7.opPattern","COPY",BODY,{"derivedFrom":makeQuery(id+"F4.opPattern","COPY",BODY,{"derivedFrom":makeQuery(id+"F1.opRevolve","SWEPT_BODY",BODY,{"disambiguationData":[OSD([sQuery(id+"F0.wireOp",EDGE,"E1")])]}),"instanceName":"1"}),"instanceName":"1"}),"instanceName":"1"});
            var Q220;
            Q220=makeQuery(id+"F10.opPattern","COPY",BODY,{"derivedFrom":makeQuery(id+"F7.opPattern","COPY",BODY,{"derivedFrom":makeQuery(id+"F4.opPattern","COPY",BODY,{"derivedFrom":makeQuery(id+"F2.opPattern","COPY",BODY,{"derivedFrom":makeQuery(id+"F1.opRevolve","SWEPT_BODY",BODY,{"disambiguationData":[OSD([sQuery(id+"F0.wireOp",EDGE,"E1")])]}),"instanceName":"1"}),"instanceName":"1"}),"instanceName":"1"}),"instanceName":"1"});
            var Q221;
            Q221=makeQuery(id+"F10.opPattern","COPY",BODY,{"derivedFrom":makeQuery(id+"F7.opPattern","COPY",BODY,{"derivedFrom":makeQuery(id+"F4.opPattern","COPY",BODY,{"derivedFrom":makeQuery(id+"F3.opPattern","COPY",BODY,{"derivedFrom":makeQuery(id+"F2.opPattern","COPY",BODY,{"derivedFrom":makeQuery(id+"F1.opRevolve","SWEPT_BODY",BODY,{"disambiguationData":[OSD([sQuery(id+"F0.wireOp",EDGE,"E1")])]}),"instanceName":"1"}),"instanceName":"1"}),"instanceName":"1"}),"instanceName":"1"}),"instanceName":"1"});
            var Q222;
            Q222=makeQuery(id+"F10.opPattern","COPY",BODY,{"derivedFrom":makeQuery(id+"F7.opPattern","COPY",BODY,{"derivedFrom":makeQuery(id+"F5.opPattern","COPY",BODY,{"derivedFrom":makeQuery(id+"F1.opRevolve","SWEPT_BODY",BODY,{"disambiguationData":[OSD([sQuery(id+"F0.wireOp",EDGE,"E1")])]}),"instanceName":"1"}),"instanceName":"1"}),"instanceName":"1"});
            var Q223;
            Q223=makeQuery(id+"F10.opPattern","COPY",BODY,{"derivedFrom":makeQuery(id+"F7.opPattern","COPY",BODY,{"derivedFrom":makeQuery(id+"F5.opPattern","COPY",BODY,{"derivedFrom":makeQuery(id+"F2.opPattern","COPY",BODY,{"derivedFrom":makeQuery(id+"F1.opRevolve","SWEPT_BODY",BODY,{"disambiguationData":[OSD([sQuery(id+"F0.wireOp",EDGE,"E1")])]}),"instanceName":"1"}),"instanceName":"1"}),"instanceName":"1"}),"instanceName":"1"});
            var Q224;
            Q224=makeQuery(id+"F10.opPattern","COPY",BODY,{"derivedFrom":makeQuery(id+"F7.opPattern","COPY",BODY,{"derivedFrom":makeQuery(id+"F5.opPattern","COPY",BODY,{"derivedFrom":makeQuery(id+"F3.opPattern","COPY",BODY,{"derivedFrom":makeQuery(id+"F2.opPattern","COPY",BODY,{"derivedFrom":makeQuery(id+"F1.opRevolve","SWEPT_BODY",BODY,{"disambiguationData":[OSD([sQuery(id+"F0.wireOp",EDGE,"E1")])]}),"instanceName":"1"}),"instanceName":"1"}),"instanceName":"1"}),"instanceName":"1"}),"instanceName":"1"});
            var Q225;
            Q225=makeQuery(id+"F10.opPattern","COPY",BODY,{"derivedFrom":makeQuery(id+"F7.opPattern","COPY",BODY,{"derivedFrom":makeQuery(id+"F5.opPattern","COPY",BODY,{"derivedFrom":makeQuery(id+"F4.opPattern","COPY",BODY,{"derivedFrom":makeQuery(id+"F1.opRevolve","SWEPT_BODY",BODY,{"disambiguationData":[OSD([sQuery(id+"F0.wireOp",EDGE,"E1")])]}),"instanceName":"1"}),"instanceName":"1"}),"instanceName":"1"}),"instanceName":"1"});
            var Q226;
            Q226=makeQuery(id+"F10.opPattern","COPY",BODY,{"derivedFrom":makeQuery(id+"F7.opPattern","COPY",BODY,{"derivedFrom":makeQuery(id+"F5.opPattern","COPY",BODY,{"derivedFrom":makeQuery(id+"F4.opPattern","COPY",BODY,{"derivedFrom":makeQuery(id+"F2.opPattern","COPY",BODY,{"derivedFrom":makeQuery(id+"F1.opRevolve","SWEPT_BODY",BODY,{"disambiguationData":[OSD([sQuery(id+"F0.wireOp",EDGE,"E1")])]}),"instanceName":"1"}),"instanceName":"1"}),"instanceName":"1"}),"instanceName":"1"}),"instanceName":"1"});
            var Q227;
            Q227=makeQuery(id+"F10.opPattern","COPY",BODY,{"derivedFrom":makeQuery(id+"F7.opPattern","COPY",BODY,{"derivedFrom":makeQuery(id+"F5.opPattern","COPY",BODY,{"derivedFrom":makeQuery(id+"F4.opPattern","COPY",BODY,{"derivedFrom":makeQuery(id+"F3.opPattern","COPY",BODY,{"derivedFrom":makeQuery(id+"F2.opPattern","COPY",BODY,{"derivedFrom":makeQuery(id+"F1.opRevolve","SWEPT_BODY",BODY,{"disambiguationData":[OSD([sQuery(id+"F0.wireOp",EDGE,"E1")])]}),"instanceName":"1"}),"instanceName":"1"}),"instanceName":"1"}),"instanceName":"1"}),"instanceName":"1"}),"instanceName":"1"});
            var Q228;
            Q228=makeQuery(id+"F10.opPattern","COPY",BODY,{"derivedFrom":makeQuery(id+"F7.opPattern","COPY",BODY,{"derivedFrom":makeQuery(id+"F6.opPattern","COPY",BODY,{"derivedFrom":makeQuery(id+"F1.opRevolve","SWEPT_BODY",BODY,{"disambiguationData":[OSD([sQuery(id+"F0.wireOp",EDGE,"E1")])]}),"instanceName":"1"}),"instanceName":"1"}),"instanceName":"1"});
            var Q229;
            Q229=makeQuery(id+"F10.opPattern","COPY",BODY,{"derivedFrom":makeQuery(id+"F7.opPattern","COPY",BODY,{"derivedFrom":makeQuery(id+"F6.opPattern","COPY",BODY,{"derivedFrom":makeQuery(id+"F2.opPattern","COPY",BODY,{"derivedFrom":makeQuery(id+"F1.opRevolve","SWEPT_BODY",BODY,{"disambiguationData":[OSD([sQuery(id+"F0.wireOp",EDGE,"E1")])]}),"instanceName":"1"}),"instanceName":"1"}),"instanceName":"1"}),"instanceName":"1"});
            var Q230;
            Q230=makeQuery(id+"F10.opPattern","COPY",BODY,{"derivedFrom":makeQuery(id+"F7.opPattern","COPY",BODY,{"derivedFrom":makeQuery(id+"F6.opPattern","COPY",BODY,{"derivedFrom":makeQuery(id+"F3.opPattern","COPY",BODY,{"derivedFrom":makeQuery(id+"F2.opPattern","COPY",BODY,{"derivedFrom":makeQuery(id+"F1.opRevolve","SWEPT_BODY",BODY,{"disambiguationData":[OSD([sQuery(id+"F0.wireOp",EDGE,"E1")])]}),"instanceName":"1"}),"instanceName":"1"}),"instanceName":"1"}),"instanceName":"1"}),"instanceName":"1"});
            var Q231;
            Q231=makeQuery(id+"F10.opPattern","COPY",BODY,{"derivedFrom":makeQuery(id+"F7.opPattern","COPY",BODY,{"derivedFrom":makeQuery(id+"F6.opPattern","COPY",BODY,{"derivedFrom":makeQuery(id+"F4.opPattern","COPY",BODY,{"derivedFrom":makeQuery(id+"F1.opRevolve","SWEPT_BODY",BODY,{"disambiguationData":[OSD([sQuery(id+"F0.wireOp",EDGE,"E1")])]}),"instanceName":"1"}),"instanceName":"1"}),"instanceName":"1"}),"instanceName":"1"});
            var Q232;
            Q232=makeQuery(id+"F10.opPattern","COPY",BODY,{"derivedFrom":makeQuery(id+"F7.opPattern","COPY",BODY,{"derivedFrom":makeQuery(id+"F6.opPattern","COPY",BODY,{"derivedFrom":makeQuery(id+"F4.opPattern","COPY",BODY,{"derivedFrom":makeQuery(id+"F2.opPattern","COPY",BODY,{"derivedFrom":makeQuery(id+"F1.opRevolve","SWEPT_BODY",BODY,{"disambiguationData":[OSD([sQuery(id+"F0.wireOp",EDGE,"E1")])]}),"instanceName":"1"}),"instanceName":"1"}),"instanceName":"1"}),"instanceName":"1"}),"instanceName":"1"});
            var Q233;
            Q233=makeQuery(id+"F10.opPattern","COPY",BODY,{"derivedFrom":makeQuery(id+"F7.opPattern","COPY",BODY,{"derivedFrom":makeQuery(id+"F6.opPattern","COPY",BODY,{"derivedFrom":makeQuery(id+"F4.opPattern","COPY",BODY,{"derivedFrom":makeQuery(id+"F3.opPattern","COPY",BODY,{"derivedFrom":makeQuery(id+"F2.opPattern","COPY",BODY,{"derivedFrom":makeQuery(id+"F1.opRevolve","SWEPT_BODY",BODY,{"disambiguationData":[OSD([sQuery(id+"F0.wireOp",EDGE,"E1")])]}),"instanceName":"1"}),"instanceName":"1"}),"instanceName":"1"}),"instanceName":"1"}),"instanceName":"1"}),"instanceName":"1"});
            var Q234;
            Q234=makeQuery(id+"F10.opPattern","COPY",BODY,{"derivedFrom":makeQuery(id+"F7.opPattern","COPY",BODY,{"derivedFrom":makeQuery(id+"F6.opPattern","COPY",BODY,{"derivedFrom":makeQuery(id+"F5.opPattern","COPY",BODY,{"derivedFrom":makeQuery(id+"F1.opRevolve","SWEPT_BODY",BODY,{"disambiguationData":[OSD([sQuery(id+"F0.wireOp",EDGE,"E1")])]}),"instanceName":"1"}),"instanceName":"1"}),"instanceName":"1"}),"instanceName":"1"});
            var Q235;
            Q235=makeQuery(id+"F10.opPattern","COPY",BODY,{"derivedFrom":makeQuery(id+"F7.opPattern","COPY",BODY,{"derivedFrom":makeQuery(id+"F6.opPattern","COPY",BODY,{"derivedFrom":makeQuery(id+"F5.opPattern","COPY",BODY,{"derivedFrom":makeQuery(id+"F2.opPattern","COPY",BODY,{"derivedFrom":makeQuery(id+"F1.opRevolve","SWEPT_BODY",BODY,{"disambiguationData":[OSD([sQuery(id+"F0.wireOp",EDGE,"E1")])]}),"instanceName":"1"}),"instanceName":"1"}),"instanceName":"1"}),"instanceName":"1"}),"instanceName":"1"});
            var Q236;
            Q236=makeQuery(id+"F10.opPattern","COPY",BODY,{"derivedFrom":makeQuery(id+"F7.opPattern","COPY",BODY,{"derivedFrom":makeQuery(id+"F6.opPattern","COPY",BODY,{"derivedFrom":makeQuery(id+"F5.opPattern","COPY",BODY,{"derivedFrom":makeQuery(id+"F3.opPattern","COPY",BODY,{"derivedFrom":makeQuery(id+"F2.opPattern","COPY",BODY,{"derivedFrom":makeQuery(id+"F1.opRevolve","SWEPT_BODY",BODY,{"disambiguationData":[OSD([sQuery(id+"F0.wireOp",EDGE,"E1")])]}),"instanceName":"1"}),"instanceName":"1"}),"instanceName":"1"}),"instanceName":"1"}),"instanceName":"1"}),"instanceName":"1"});
            var Q237;
            Q237=makeQuery(id+"F10.opPattern","COPY",BODY,{"derivedFrom":makeQuery(id+"F7.opPattern","COPY",BODY,{"derivedFrom":makeQuery(id+"F6.opPattern","COPY",BODY,{"derivedFrom":makeQuery(id+"F5.opPattern","COPY",BODY,{"derivedFrom":makeQuery(id+"F4.opPattern","COPY",BODY,{"derivedFrom":makeQuery(id+"F1.opRevolve","SWEPT_BODY",BODY,{"disambiguationData":[OSD([sQuery(id+"F0.wireOp",EDGE,"E1")])]}),"instanceName":"1"}),"instanceName":"1"}),"instanceName":"1"}),"instanceName":"1"}),"instanceName":"1"});
            var Q238;
            Q238=makeQuery(id+"F10.opPattern","COPY",BODY,{"derivedFrom":makeQuery(id+"F7.opPattern","COPY",BODY,{"derivedFrom":makeQuery(id+"F6.opPattern","COPY",BODY,{"derivedFrom":makeQuery(id+"F5.opPattern","COPY",BODY,{"derivedFrom":makeQuery(id+"F4.opPattern","COPY",BODY,{"derivedFrom":makeQuery(id+"F2.opPattern","COPY",BODY,{"derivedFrom":makeQuery(id+"F1.opRevolve","SWEPT_BODY",BODY,{"disambiguationData":[OSD([sQuery(id+"F0.wireOp",EDGE,"E1")])]}),"instanceName":"1"}),"instanceName":"1"}),"instanceName":"1"}),"instanceName":"1"}),"instanceName":"1"}),"instanceName":"1"});
            var Q239;
            Q239=makeQuery(id+"F10.opPattern","COPY",BODY,{"derivedFrom":makeQuery(id+"F7.opPattern","COPY",BODY,{"derivedFrom":makeQuery(id+"F6.opPattern","COPY",BODY,{"derivedFrom":makeQuery(id+"F5.opPattern","COPY",BODY,{"derivedFrom":makeQuery(id+"F4.opPattern","COPY",BODY,{"derivedFrom":makeQuery(id+"F3.opPattern","COPY",BODY,{"derivedFrom":makeQuery(id+"F2.opPattern","COPY",BODY,{"derivedFrom":makeQuery(id+"F1.opRevolve","SWEPT_BODY",BODY,{"disambiguationData":[OSD([sQuery(id+"F0.wireOp",EDGE,"E1")])]}),"instanceName":"1"}),"instanceName":"1"}),"instanceName":"1"}),"instanceName":"1"}),"instanceName":"1"}),"instanceName":"1"}),"instanceName":"1"});
            var Q240;
            Q240=makeQuery(id+"F10.opPattern","COPY",BODY,{"derivedFrom":makeQuery(id+"F8.opPattern","COPY",BODY,{"derivedFrom":makeQuery(id+"F1.opRevolve","SWEPT_BODY",BODY,{"disambiguationData":[OSD([sQuery(id+"F0.wireOp",EDGE,"E1")])]}),"instanceName":"1"}),"instanceName":"1"});
            var Q241;
            Q241=makeQuery(id+"F10.opPattern","COPY",BODY,{"derivedFrom":makeQuery(id+"F8.opPattern","COPY",BODY,{"derivedFrom":makeQuery(id+"F2.opPattern","COPY",BODY,{"derivedFrom":makeQuery(id+"F1.opRevolve","SWEPT_BODY",BODY,{"disambiguationData":[OSD([sQuery(id+"F0.wireOp",EDGE,"E1")])]}),"instanceName":"1"}),"instanceName":"1"}),"instanceName":"1"});
            var Q242;
            Q242=makeQuery(id+"F10.opPattern","COPY",BODY,{"derivedFrom":makeQuery(id+"F8.opPattern","COPY",BODY,{"derivedFrom":makeQuery(id+"F3.opPattern","COPY",BODY,{"derivedFrom":makeQuery(id+"F2.opPattern","COPY",BODY,{"derivedFrom":makeQuery(id+"F1.opRevolve","SWEPT_BODY",BODY,{"disambiguationData":[OSD([sQuery(id+"F0.wireOp",EDGE,"E1")])]}),"instanceName":"1"}),"instanceName":"1"}),"instanceName":"1"}),"instanceName":"1"});
            var Q243;
            Q243=makeQuery(id+"F10.opPattern","COPY",BODY,{"derivedFrom":makeQuery(id+"F8.opPattern","COPY",BODY,{"derivedFrom":makeQuery(id+"F4.opPattern","COPY",BODY,{"derivedFrom":makeQuery(id+"F1.opRevolve","SWEPT_BODY",BODY,{"disambiguationData":[OSD([sQuery(id+"F0.wireOp",EDGE,"E1")])]}),"instanceName":"1"}),"instanceName":"1"}),"instanceName":"1"});
            var Q244;
            Q244=makeQuery(id+"F10.opPattern","COPY",BODY,{"derivedFrom":makeQuery(id+"F8.opPattern","COPY",BODY,{"derivedFrom":makeQuery(id+"F4.opPattern","COPY",BODY,{"derivedFrom":makeQuery(id+"F2.opPattern","COPY",BODY,{"derivedFrom":makeQuery(id+"F1.opRevolve","SWEPT_BODY",BODY,{"disambiguationData":[OSD([sQuery(id+"F0.wireOp",EDGE,"E1")])]}),"instanceName":"1"}),"instanceName":"1"}),"instanceName":"1"}),"instanceName":"1"});
            var Q245;
            Q245=makeQuery(id+"F10.opPattern","COPY",BODY,{"derivedFrom":makeQuery(id+"F8.opPattern","COPY",BODY,{"derivedFrom":makeQuery(id+"F4.opPattern","COPY",BODY,{"derivedFrom":makeQuery(id+"F3.opPattern","COPY",BODY,{"derivedFrom":makeQuery(id+"F2.opPattern","COPY",BODY,{"derivedFrom":makeQuery(id+"F1.opRevolve","SWEPT_BODY",BODY,{"disambiguationData":[OSD([sQuery(id+"F0.wireOp",EDGE,"E1")])]}),"instanceName":"1"}),"instanceName":"1"}),"instanceName":"1"}),"instanceName":"1"}),"instanceName":"1"});
            var Q246;
            Q246=makeQuery(id+"F10.opPattern","COPY",BODY,{"derivedFrom":makeQuery(id+"F8.opPattern","COPY",BODY,{"derivedFrom":makeQuery(id+"F5.opPattern","COPY",BODY,{"derivedFrom":makeQuery(id+"F1.opRevolve","SWEPT_BODY",BODY,{"disambiguationData":[OSD([sQuery(id+"F0.wireOp",EDGE,"E1")])]}),"instanceName":"1"}),"instanceName":"1"}),"instanceName":"1"});
            var Q247;
            Q247=makeQuery(id+"F10.opPattern","COPY",BODY,{"derivedFrom":makeQuery(id+"F8.opPattern","COPY",BODY,{"derivedFrom":makeQuery(id+"F5.opPattern","COPY",BODY,{"derivedFrom":makeQuery(id+"F2.opPattern","COPY",BODY,{"derivedFrom":makeQuery(id+"F1.opRevolve","SWEPT_BODY",BODY,{"disambiguationData":[OSD([sQuery(id+"F0.wireOp",EDGE,"E1")])]}),"instanceName":"1"}),"instanceName":"1"}),"instanceName":"1"}),"instanceName":"1"});
            var Q248;
            Q248=makeQuery(id+"F10.opPattern","COPY",BODY,{"derivedFrom":makeQuery(id+"F8.opPattern","COPY",BODY,{"derivedFrom":makeQuery(id+"F5.opPattern","COPY",BODY,{"derivedFrom":makeQuery(id+"F3.opPattern","COPY",BODY,{"derivedFrom":makeQuery(id+"F2.opPattern","COPY",BODY,{"derivedFrom":makeQuery(id+"F1.opRevolve","SWEPT_BODY",BODY,{"disambiguationData":[OSD([sQuery(id+"F0.wireOp",EDGE,"E1")])]}),"instanceName":"1"}),"instanceName":"1"}),"instanceName":"1"}),"instanceName":"1"}),"instanceName":"1"});
            var Q249;
            Q249=makeQuery(id+"F10.opPattern","COPY",BODY,{"derivedFrom":makeQuery(id+"F8.opPattern","COPY",BODY,{"derivedFrom":makeQuery(id+"F5.opPattern","COPY",BODY,{"derivedFrom":makeQuery(id+"F4.opPattern","COPY",BODY,{"derivedFrom":makeQuery(id+"F1.opRevolve","SWEPT_BODY",BODY,{"disambiguationData":[OSD([sQuery(id+"F0.wireOp",EDGE,"E1")])]}),"instanceName":"1"}),"instanceName":"1"}),"instanceName":"1"}),"instanceName":"1"});
            var Q250;
            Q250=makeQuery(id+"F10.opPattern","COPY",BODY,{"derivedFrom":makeQuery(id+"F8.opPattern","COPY",BODY,{"derivedFrom":makeQuery(id+"F5.opPattern","COPY",BODY,{"derivedFrom":makeQuery(id+"F4.opPattern","COPY",BODY,{"derivedFrom":makeQuery(id+"F2.opPattern","COPY",BODY,{"derivedFrom":makeQuery(id+"F1.opRevolve","SWEPT_BODY",BODY,{"disambiguationData":[OSD([sQuery(id+"F0.wireOp",EDGE,"E1")])]}),"instanceName":"1"}),"instanceName":"1"}),"instanceName":"1"}),"instanceName":"1"}),"instanceName":"1"});
            var Q251;
            Q251=makeQuery(id+"F10.opPattern","COPY",BODY,{"derivedFrom":makeQuery(id+"F8.opPattern","COPY",BODY,{"derivedFrom":makeQuery(id+"F5.opPattern","COPY",BODY,{"derivedFrom":makeQuery(id+"F4.opPattern","COPY",BODY,{"derivedFrom":makeQuery(id+"F3.opPattern","COPY",BODY,{"derivedFrom":makeQuery(id+"F2.opPattern","COPY",BODY,{"derivedFrom":makeQuery(id+"F1.opRevolve","SWEPT_BODY",BODY,{"disambiguationData":[OSD([sQuery(id+"F0.wireOp",EDGE,"E1")])]}),"instanceName":"1"}),"instanceName":"1"}),"instanceName":"1"}),"instanceName":"1"}),"instanceName":"1"}),"instanceName":"1"});
            var Q252;
            Q252=makeQuery(id+"F10.opPattern","COPY",BODY,{"derivedFrom":makeQuery(id+"F8.opPattern","COPY",BODY,{"derivedFrom":makeQuery(id+"F6.opPattern","COPY",BODY,{"derivedFrom":makeQuery(id+"F1.opRevolve","SWEPT_BODY",BODY,{"disambiguationData":[OSD([sQuery(id+"F0.wireOp",EDGE,"E1")])]}),"instanceName":"1"}),"instanceName":"1"}),"instanceName":"1"});
            var Q253;
            Q253=makeQuery(id+"F10.opPattern","COPY",BODY,{"derivedFrom":makeQuery(id+"F8.opPattern","COPY",BODY,{"derivedFrom":makeQuery(id+"F6.opPattern","COPY",BODY,{"derivedFrom":makeQuery(id+"F2.opPattern","COPY",BODY,{"derivedFrom":makeQuery(id+"F1.opRevolve","SWEPT_BODY",BODY,{"disambiguationData":[OSD([sQuery(id+"F0.wireOp",EDGE,"E1")])]}),"instanceName":"1"}),"instanceName":"1"}),"instanceName":"1"}),"instanceName":"1"});
            var Q254;
            Q254=makeQuery(id+"F10.opPattern","COPY",BODY,{"derivedFrom":makeQuery(id+"F8.opPattern","COPY",BODY,{"derivedFrom":makeQuery(id+"F6.opPattern","COPY",BODY,{"derivedFrom":makeQuery(id+"F3.opPattern","COPY",BODY,{"derivedFrom":makeQuery(id+"F2.opPattern","COPY",BODY,{"derivedFrom":makeQuery(id+"F1.opRevolve","SWEPT_BODY",BODY,{"disambiguationData":[OSD([sQuery(id+"F0.wireOp",EDGE,"E1")])]}),"instanceName":"1"}),"instanceName":"1"}),"instanceName":"1"}),"instanceName":"1"}),"instanceName":"1"});
            var Q255;
            Q255=makeQuery(id+"F10.opPattern","COPY",BODY,{"derivedFrom":makeQuery(id+"F8.opPattern","COPY",BODY,{"derivedFrom":makeQuery(id+"F6.opPattern","COPY",BODY,{"derivedFrom":makeQuery(id+"F4.opPattern","COPY",BODY,{"derivedFrom":makeQuery(id+"F1.opRevolve","SWEPT_BODY",BODY,{"disambiguationData":[OSD([sQuery(id+"F0.wireOp",EDGE,"E1")])]}),"instanceName":"1"}),"instanceName":"1"}),"instanceName":"1"}),"instanceName":"1"});
            var Q256;
            Q256=makeQuery(id+"F10.opPattern","COPY",BODY,{"derivedFrom":makeQuery(id+"F8.opPattern","COPY",BODY,{"derivedFrom":makeQuery(id+"F6.opPattern","COPY",BODY,{"derivedFrom":makeQuery(id+"F4.opPattern","COPY",BODY,{"derivedFrom":makeQuery(id+"F2.opPattern","COPY",BODY,{"derivedFrom":makeQuery(id+"F1.opRevolve","SWEPT_BODY",BODY,{"disambiguationData":[OSD([sQuery(id+"F0.wireOp",EDGE,"E1")])]}),"instanceName":"1"}),"instanceName":"1"}),"instanceName":"1"}),"instanceName":"1"}),"instanceName":"1"});
            var Q257;
            Q257=makeQuery(id+"F10.opPattern","COPY",BODY,{"derivedFrom":makeQuery(id+"F8.opPattern","COPY",BODY,{"derivedFrom":makeQuery(id+"F6.opPattern","COPY",BODY,{"derivedFrom":makeQuery(id+"F4.opPattern","COPY",BODY,{"derivedFrom":makeQuery(id+"F3.opPattern","COPY",BODY,{"derivedFrom":makeQuery(id+"F2.opPattern","COPY",BODY,{"derivedFrom":makeQuery(id+"F1.opRevolve","SWEPT_BODY",BODY,{"disambiguationData":[OSD([sQuery(id+"F0.wireOp",EDGE,"E1")])]}),"instanceName":"1"}),"instanceName":"1"}),"instanceName":"1"}),"instanceName":"1"}),"instanceName":"1"}),"instanceName":"1"});
            var Q258;
            Q258=makeQuery(id+"F10.opPattern","COPY",BODY,{"derivedFrom":makeQuery(id+"F8.opPattern","COPY",BODY,{"derivedFrom":makeQuery(id+"F6.opPattern","COPY",BODY,{"derivedFrom":makeQuery(id+"F5.opPattern","COPY",BODY,{"derivedFrom":makeQuery(id+"F1.opRevolve","SWEPT_BODY",BODY,{"disambiguationData":[OSD([sQuery(id+"F0.wireOp",EDGE,"E1")])]}),"instanceName":"1"}),"instanceName":"1"}),"instanceName":"1"}),"instanceName":"1"});
            var Q259;
            Q259=makeQuery(id+"F10.opPattern","COPY",BODY,{"derivedFrom":makeQuery(id+"F8.opPattern","COPY",BODY,{"derivedFrom":makeQuery(id+"F6.opPattern","COPY",BODY,{"derivedFrom":makeQuery(id+"F5.opPattern","COPY",BODY,{"derivedFrom":makeQuery(id+"F2.opPattern","COPY",BODY,{"derivedFrom":makeQuery(id+"F1.opRevolve","SWEPT_BODY",BODY,{"disambiguationData":[OSD([sQuery(id+"F0.wireOp",EDGE,"E1")])]}),"instanceName":"1"}),"instanceName":"1"}),"instanceName":"1"}),"instanceName":"1"}),"instanceName":"1"});
            var Q260;
            Q260=makeQuery(id+"F10.opPattern","COPY",BODY,{"derivedFrom":makeQuery(id+"F8.opPattern","COPY",BODY,{"derivedFrom":makeQuery(id+"F6.opPattern","COPY",BODY,{"derivedFrom":makeQuery(id+"F5.opPattern","COPY",BODY,{"derivedFrom":makeQuery(id+"F3.opPattern","COPY",BODY,{"derivedFrom":makeQuery(id+"F2.opPattern","COPY",BODY,{"derivedFrom":makeQuery(id+"F1.opRevolve","SWEPT_BODY",BODY,{"disambiguationData":[OSD([sQuery(id+"F0.wireOp",EDGE,"E1")])]}),"instanceName":"1"}),"instanceName":"1"}),"instanceName":"1"}),"instanceName":"1"}),"instanceName":"1"}),"instanceName":"1"});
            var Q261;
            Q261=makeQuery(id+"F10.opPattern","COPY",BODY,{"derivedFrom":makeQuery(id+"F8.opPattern","COPY",BODY,{"derivedFrom":makeQuery(id+"F6.opPattern","COPY",BODY,{"derivedFrom":makeQuery(id+"F5.opPattern","COPY",BODY,{"derivedFrom":makeQuery(id+"F4.opPattern","COPY",BODY,{"derivedFrom":makeQuery(id+"F1.opRevolve","SWEPT_BODY",BODY,{"disambiguationData":[OSD([sQuery(id+"F0.wireOp",EDGE,"E1")])]}),"instanceName":"1"}),"instanceName":"1"}),"instanceName":"1"}),"instanceName":"1"}),"instanceName":"1"});
            var Q262;
            Q262=makeQuery(id+"F10.opPattern","COPY",BODY,{"derivedFrom":makeQuery(id+"F8.opPattern","COPY",BODY,{"derivedFrom":makeQuery(id+"F6.opPattern","COPY",BODY,{"derivedFrom":makeQuery(id+"F5.opPattern","COPY",BODY,{"derivedFrom":makeQuery(id+"F4.opPattern","COPY",BODY,{"derivedFrom":makeQuery(id+"F2.opPattern","COPY",BODY,{"derivedFrom":makeQuery(id+"F1.opRevolve","SWEPT_BODY",BODY,{"disambiguationData":[OSD([sQuery(id+"F0.wireOp",EDGE,"E1")])]}),"instanceName":"1"}),"instanceName":"1"}),"instanceName":"1"}),"instanceName":"1"}),"instanceName":"1"}),"instanceName":"1"});
            var Q263;
            Q263=makeQuery(id+"F10.opPattern","COPY",BODY,{"derivedFrom":makeQuery(id+"F8.opPattern","COPY",BODY,{"derivedFrom":makeQuery(id+"F6.opPattern","COPY",BODY,{"derivedFrom":makeQuery(id+"F5.opPattern","COPY",BODY,{"derivedFrom":makeQuery(id+"F4.opPattern","COPY",BODY,{"derivedFrom":makeQuery(id+"F3.opPattern","COPY",BODY,{"derivedFrom":makeQuery(id+"F2.opPattern","COPY",BODY,{"derivedFrom":makeQuery(id+"F1.opRevolve","SWEPT_BODY",BODY,{"disambiguationData":[OSD([sQuery(id+"F0.wireOp",EDGE,"E1")])]}),"instanceName":"1"}),"instanceName":"1"}),"instanceName":"1"}),"instanceName":"1"}),"instanceName":"1"}),"instanceName":"1"}),"instanceName":"1"});
            var Q264;
            Q264=makeQuery(id+"F10.opPattern","COPY",BODY,{"derivedFrom":makeQuery(id+"F8.opPattern","COPY",BODY,{"derivedFrom":makeQuery(id+"F7.opPattern","COPY",BODY,{"derivedFrom":makeQuery(id+"F1.opRevolve","SWEPT_BODY",BODY,{"disambiguationData":[OSD([sQuery(id+"F0.wireOp",EDGE,"E1")])]}),"instanceName":"1"}),"instanceName":"1"}),"instanceName":"1"});
            var Q265;
            Q265=makeQuery(id+"F10.opPattern","COPY",BODY,{"derivedFrom":makeQuery(id+"F8.opPattern","COPY",BODY,{"derivedFrom":makeQuery(id+"F7.opPattern","COPY",BODY,{"derivedFrom":makeQuery(id+"F2.opPattern","COPY",BODY,{"derivedFrom":makeQuery(id+"F1.opRevolve","SWEPT_BODY",BODY,{"disambiguationData":[OSD([sQuery(id+"F0.wireOp",EDGE,"E1")])]}),"instanceName":"1"}),"instanceName":"1"}),"instanceName":"1"}),"instanceName":"1"});
            var Q266;
            Q266=makeQuery(id+"F10.opPattern","COPY",BODY,{"derivedFrom":makeQuery(id+"F8.opPattern","COPY",BODY,{"derivedFrom":makeQuery(id+"F7.opPattern","COPY",BODY,{"derivedFrom":makeQuery(id+"F3.opPattern","COPY",BODY,{"derivedFrom":makeQuery(id+"F2.opPattern","COPY",BODY,{"derivedFrom":makeQuery(id+"F1.opRevolve","SWEPT_BODY",BODY,{"disambiguationData":[OSD([sQuery(id+"F0.wireOp",EDGE,"E1")])]}),"instanceName":"1"}),"instanceName":"1"}),"instanceName":"1"}),"instanceName":"1"}),"instanceName":"1"});
            var Q267;
            Q267=makeQuery(id+"F10.opPattern","COPY",BODY,{"derivedFrom":makeQuery(id+"F8.opPattern","COPY",BODY,{"derivedFrom":makeQuery(id+"F7.opPattern","COPY",BODY,{"derivedFrom":makeQuery(id+"F4.opPattern","COPY",BODY,{"derivedFrom":makeQuery(id+"F1.opRevolve","SWEPT_BODY",BODY,{"disambiguationData":[OSD([sQuery(id+"F0.wireOp",EDGE,"E1")])]}),"instanceName":"1"}),"instanceName":"1"}),"instanceName":"1"}),"instanceName":"1"});
            var Q268;
            Q268=makeQuery(id+"F10.opPattern","COPY",BODY,{"derivedFrom":makeQuery(id+"F8.opPattern","COPY",BODY,{"derivedFrom":makeQuery(id+"F7.opPattern","COPY",BODY,{"derivedFrom":makeQuery(id+"F4.opPattern","COPY",BODY,{"derivedFrom":makeQuery(id+"F2.opPattern","COPY",BODY,{"derivedFrom":makeQuery(id+"F1.opRevolve","SWEPT_BODY",BODY,{"disambiguationData":[OSD([sQuery(id+"F0.wireOp",EDGE,"E1")])]}),"instanceName":"1"}),"instanceName":"1"}),"instanceName":"1"}),"instanceName":"1"}),"instanceName":"1"});
            var Q269;
            Q269=makeQuery(id+"F10.opPattern","COPY",BODY,{"derivedFrom":makeQuery(id+"F8.opPattern","COPY",BODY,{"derivedFrom":makeQuery(id+"F7.opPattern","COPY",BODY,{"derivedFrom":makeQuery(id+"F4.opPattern","COPY",BODY,{"derivedFrom":makeQuery(id+"F3.opPattern","COPY",BODY,{"derivedFrom":makeQuery(id+"F2.opPattern","COPY",BODY,{"derivedFrom":makeQuery(id+"F1.opRevolve","SWEPT_BODY",BODY,{"disambiguationData":[OSD([sQuery(id+"F0.wireOp",EDGE,"E1")])]}),"instanceName":"1"}),"instanceName":"1"}),"instanceName":"1"}),"instanceName":"1"}),"instanceName":"1"}),"instanceName":"1"});
            var Q270;
            Q270=makeQuery(id+"F10.opPattern","COPY",BODY,{"derivedFrom":makeQuery(id+"F8.opPattern","COPY",BODY,{"derivedFrom":makeQuery(id+"F7.opPattern","COPY",BODY,{"derivedFrom":makeQuery(id+"F5.opPattern","COPY",BODY,{"derivedFrom":makeQuery(id+"F1.opRevolve","SWEPT_BODY",BODY,{"disambiguationData":[OSD([sQuery(id+"F0.wireOp",EDGE,"E1")])]}),"instanceName":"1"}),"instanceName":"1"}),"instanceName":"1"}),"instanceName":"1"});
            var Q271;
            Q271=makeQuery(id+"F10.opPattern","COPY",BODY,{"derivedFrom":makeQuery(id+"F8.opPattern","COPY",BODY,{"derivedFrom":makeQuery(id+"F7.opPattern","COPY",BODY,{"derivedFrom":makeQuery(id+"F5.opPattern","COPY",BODY,{"derivedFrom":makeQuery(id+"F2.opPattern","COPY",BODY,{"derivedFrom":makeQuery(id+"F1.opRevolve","SWEPT_BODY",BODY,{"disambiguationData":[OSD([sQuery(id+"F0.wireOp",EDGE,"E1")])]}),"instanceName":"1"}),"instanceName":"1"}),"instanceName":"1"}),"instanceName":"1"}),"instanceName":"1"});
            var Q272;
            Q272=makeQuery(id+"F10.opPattern","COPY",BODY,{"derivedFrom":makeQuery(id+"F8.opPattern","COPY",BODY,{"derivedFrom":makeQuery(id+"F7.opPattern","COPY",BODY,{"derivedFrom":makeQuery(id+"F5.opPattern","COPY",BODY,{"derivedFrom":makeQuery(id+"F3.opPattern","COPY",BODY,{"derivedFrom":makeQuery(id+"F2.opPattern","COPY",BODY,{"derivedFrom":makeQuery(id+"F1.opRevolve","SWEPT_BODY",BODY,{"disambiguationData":[OSD([sQuery(id+"F0.wireOp",EDGE,"E1")])]}),"instanceName":"1"}),"instanceName":"1"}),"instanceName":"1"}),"instanceName":"1"}),"instanceName":"1"}),"instanceName":"1"});
            var Q273;
            Q273=makeQuery(id+"F10.opPattern","COPY",BODY,{"derivedFrom":makeQuery(id+"F8.opPattern","COPY",BODY,{"derivedFrom":makeQuery(id+"F7.opPattern","COPY",BODY,{"derivedFrom":makeQuery(id+"F5.opPattern","COPY",BODY,{"derivedFrom":makeQuery(id+"F4.opPattern","COPY",BODY,{"derivedFrom":makeQuery(id+"F1.opRevolve","SWEPT_BODY",BODY,{"disambiguationData":[OSD([sQuery(id+"F0.wireOp",EDGE,"E1")])]}),"instanceName":"1"}),"instanceName":"1"}),"instanceName":"1"}),"instanceName":"1"}),"instanceName":"1"});
            var Q274;
            Q274=makeQuery(id+"F10.opPattern","COPY",BODY,{"derivedFrom":makeQuery(id+"F8.opPattern","COPY",BODY,{"derivedFrom":makeQuery(id+"F7.opPattern","COPY",BODY,{"derivedFrom":makeQuery(id+"F5.opPattern","COPY",BODY,{"derivedFrom":makeQuery(id+"F4.opPattern","COPY",BODY,{"derivedFrom":makeQuery(id+"F2.opPattern","COPY",BODY,{"derivedFrom":makeQuery(id+"F1.opRevolve","SWEPT_BODY",BODY,{"disambiguationData":[OSD([sQuery(id+"F0.wireOp",EDGE,"E1")])]}),"instanceName":"1"}),"instanceName":"1"}),"instanceName":"1"}),"instanceName":"1"}),"instanceName":"1"}),"instanceName":"1"});
            var Q275;
            Q275=makeQuery(id+"F10.opPattern","COPY",BODY,{"derivedFrom":makeQuery(id+"F8.opPattern","COPY",BODY,{"derivedFrom":makeQuery(id+"F7.opPattern","COPY",BODY,{"derivedFrom":makeQuery(id+"F5.opPattern","COPY",BODY,{"derivedFrom":makeQuery(id+"F4.opPattern","COPY",BODY,{"derivedFrom":makeQuery(id+"F3.opPattern","COPY",BODY,{"derivedFrom":makeQuery(id+"F2.opPattern","COPY",BODY,{"derivedFrom":makeQuery(id+"F1.opRevolve","SWEPT_BODY",BODY,{"disambiguationData":[OSD([sQuery(id+"F0.wireOp",EDGE,"E1")])]}),"instanceName":"1"}),"instanceName":"1"}),"instanceName":"1"}),"instanceName":"1"}),"instanceName":"1"}),"instanceName":"1"}),"instanceName":"1"});
            var Q276;
            Q276=makeQuery(id+"F10.opPattern","COPY",BODY,{"derivedFrom":makeQuery(id+"F8.opPattern","COPY",BODY,{"derivedFrom":makeQuery(id+"F7.opPattern","COPY",BODY,{"derivedFrom":makeQuery(id+"F6.opPattern","COPY",BODY,{"derivedFrom":makeQuery(id+"F1.opRevolve","SWEPT_BODY",BODY,{"disambiguationData":[OSD([sQuery(id+"F0.wireOp",EDGE,"E1")])]}),"instanceName":"1"}),"instanceName":"1"}),"instanceName":"1"}),"instanceName":"1"});
            var Q277;
            Q277=makeQuery(id+"F10.opPattern","COPY",BODY,{"derivedFrom":makeQuery(id+"F8.opPattern","COPY",BODY,{"derivedFrom":makeQuery(id+"F7.opPattern","COPY",BODY,{"derivedFrom":makeQuery(id+"F6.opPattern","COPY",BODY,{"derivedFrom":makeQuery(id+"F2.opPattern","COPY",BODY,{"derivedFrom":makeQuery(id+"F1.opRevolve","SWEPT_BODY",BODY,{"disambiguationData":[OSD([sQuery(id+"F0.wireOp",EDGE,"E1")])]}),"instanceName":"1"}),"instanceName":"1"}),"instanceName":"1"}),"instanceName":"1"}),"instanceName":"1"});
            var Q278;
            Q278=makeQuery(id+"F10.opPattern","COPY",BODY,{"derivedFrom":makeQuery(id+"F8.opPattern","COPY",BODY,{"derivedFrom":makeQuery(id+"F7.opPattern","COPY",BODY,{"derivedFrom":makeQuery(id+"F6.opPattern","COPY",BODY,{"derivedFrom":makeQuery(id+"F3.opPattern","COPY",BODY,{"derivedFrom":makeQuery(id+"F2.opPattern","COPY",BODY,{"derivedFrom":makeQuery(id+"F1.opRevolve","SWEPT_BODY",BODY,{"disambiguationData":[OSD([sQuery(id+"F0.wireOp",EDGE,"E1")])]}),"instanceName":"1"}),"instanceName":"1"}),"instanceName":"1"}),"instanceName":"1"}),"instanceName":"1"}),"instanceName":"1"});
            var Q279;
            Q279=makeQuery(id+"F10.opPattern","COPY",BODY,{"derivedFrom":makeQuery(id+"F8.opPattern","COPY",BODY,{"derivedFrom":makeQuery(id+"F7.opPattern","COPY",BODY,{"derivedFrom":makeQuery(id+"F6.opPattern","COPY",BODY,{"derivedFrom":makeQuery(id+"F4.opPattern","COPY",BODY,{"derivedFrom":makeQuery(id+"F1.opRevolve","SWEPT_BODY",BODY,{"disambiguationData":[OSD([sQuery(id+"F0.wireOp",EDGE,"E1")])]}),"instanceName":"1"}),"instanceName":"1"}),"instanceName":"1"}),"instanceName":"1"}),"instanceName":"1"});
            var Q280;
            Q280=makeQuery(id+"F10.opPattern","COPY",BODY,{"derivedFrom":makeQuery(id+"F8.opPattern","COPY",BODY,{"derivedFrom":makeQuery(id+"F7.opPattern","COPY",BODY,{"derivedFrom":makeQuery(id+"F6.opPattern","COPY",BODY,{"derivedFrom":makeQuery(id+"F4.opPattern","COPY",BODY,{"derivedFrom":makeQuery(id+"F2.opPattern","COPY",BODY,{"derivedFrom":makeQuery(id+"F1.opRevolve","SWEPT_BODY",BODY,{"disambiguationData":[OSD([sQuery(id+"F0.wireOp",EDGE,"E1")])]}),"instanceName":"1"}),"instanceName":"1"}),"instanceName":"1"}),"instanceName":"1"}),"instanceName":"1"}),"instanceName":"1"});
            var Q281;
            Q281=makeQuery(id+"F10.opPattern","COPY",BODY,{"derivedFrom":makeQuery(id+"F8.opPattern","COPY",BODY,{"derivedFrom":makeQuery(id+"F7.opPattern","COPY",BODY,{"derivedFrom":makeQuery(id+"F6.opPattern","COPY",BODY,{"derivedFrom":makeQuery(id+"F4.opPattern","COPY",BODY,{"derivedFrom":makeQuery(id+"F3.opPattern","COPY",BODY,{"derivedFrom":makeQuery(id+"F2.opPattern","COPY",BODY,{"derivedFrom":makeQuery(id+"F1.opRevolve","SWEPT_BODY",BODY,{"disambiguationData":[OSD([sQuery(id+"F0.wireOp",EDGE,"E1")])]}),"instanceName":"1"}),"instanceName":"1"}),"instanceName":"1"}),"instanceName":"1"}),"instanceName":"1"}),"instanceName":"1"}),"instanceName":"1"});
            var Q282;
            Q282=makeQuery(id+"F10.opPattern","COPY",BODY,{"derivedFrom":makeQuery(id+"F8.opPattern","COPY",BODY,{"derivedFrom":makeQuery(id+"F7.opPattern","COPY",BODY,{"derivedFrom":makeQuery(id+"F6.opPattern","COPY",BODY,{"derivedFrom":makeQuery(id+"F5.opPattern","COPY",BODY,{"derivedFrom":makeQuery(id+"F1.opRevolve","SWEPT_BODY",BODY,{"disambiguationData":[OSD([sQuery(id+"F0.wireOp",EDGE,"E1")])]}),"instanceName":"1"}),"instanceName":"1"}),"instanceName":"1"}),"instanceName":"1"}),"instanceName":"1"});
            var Q283;
            Q283=makeQuery(id+"F10.opPattern","COPY",BODY,{"derivedFrom":makeQuery(id+"F8.opPattern","COPY",BODY,{"derivedFrom":makeQuery(id+"F7.opPattern","COPY",BODY,{"derivedFrom":makeQuery(id+"F6.opPattern","COPY",BODY,{"derivedFrom":makeQuery(id+"F5.opPattern","COPY",BODY,{"derivedFrom":makeQuery(id+"F2.opPattern","COPY",BODY,{"derivedFrom":makeQuery(id+"F1.opRevolve","SWEPT_BODY",BODY,{"disambiguationData":[OSD([sQuery(id+"F0.wireOp",EDGE,"E1")])]}),"instanceName":"1"}),"instanceName":"1"}),"instanceName":"1"}),"instanceName":"1"}),"instanceName":"1"}),"instanceName":"1"});
            var Q284;
            Q284=makeQuery(id+"F10.opPattern","COPY",BODY,{"derivedFrom":makeQuery(id+"F8.opPattern","COPY",BODY,{"derivedFrom":makeQuery(id+"F7.opPattern","COPY",BODY,{"derivedFrom":makeQuery(id+"F6.opPattern","COPY",BODY,{"derivedFrom":makeQuery(id+"F5.opPattern","COPY",BODY,{"derivedFrom":makeQuery(id+"F3.opPattern","COPY",BODY,{"derivedFrom":makeQuery(id+"F2.opPattern","COPY",BODY,{"derivedFrom":makeQuery(id+"F1.opRevolve","SWEPT_BODY",BODY,{"disambiguationData":[OSD([sQuery(id+"F0.wireOp",EDGE,"E1")])]}),"instanceName":"1"}),"instanceName":"1"}),"instanceName":"1"}),"instanceName":"1"}),"instanceName":"1"}),"instanceName":"1"}),"instanceName":"1"});
            var Q285;
            Q285=makeQuery(id+"F10.opPattern","COPY",BODY,{"derivedFrom":makeQuery(id+"F8.opPattern","COPY",BODY,{"derivedFrom":makeQuery(id+"F7.opPattern","COPY",BODY,{"derivedFrom":makeQuery(id+"F6.opPattern","COPY",BODY,{"derivedFrom":makeQuery(id+"F5.opPattern","COPY",BODY,{"derivedFrom":makeQuery(id+"F4.opPattern","COPY",BODY,{"derivedFrom":makeQuery(id+"F1.opRevolve","SWEPT_BODY",BODY,{"disambiguationData":[OSD([sQuery(id+"F0.wireOp",EDGE,"E1")])]}),"instanceName":"1"}),"instanceName":"1"}),"instanceName":"1"}),"instanceName":"1"}),"instanceName":"1"}),"instanceName":"1"});
            var Q286;
            Q286=makeQuery(id+"F10.opPattern","COPY",BODY,{"derivedFrom":makeQuery(id+"F8.opPattern","COPY",BODY,{"derivedFrom":makeQuery(id+"F7.opPattern","COPY",BODY,{"derivedFrom":makeQuery(id+"F6.opPattern","COPY",BODY,{"derivedFrom":makeQuery(id+"F5.opPattern","COPY",BODY,{"derivedFrom":makeQuery(id+"F4.opPattern","COPY",BODY,{"derivedFrom":makeQuery(id+"F2.opPattern","COPY",BODY,{"derivedFrom":makeQuery(id+"F1.opRevolve","SWEPT_BODY",BODY,{"disambiguationData":[OSD([sQuery(id+"F0.wireOp",EDGE,"E1")])]}),"instanceName":"1"}),"instanceName":"1"}),"instanceName":"1"}),"instanceName":"1"}),"instanceName":"1"}),"instanceName":"1"}),"instanceName":"1"});
            var Q287;
            Q287=makeQuery(id+"F10.opPattern","COPY",BODY,{"derivedFrom":makeQuery(id+"F8.opPattern","COPY",BODY,{"derivedFrom":makeQuery(id+"F7.opPattern","COPY",BODY,{"derivedFrom":makeQuery(id+"F6.opPattern","COPY",BODY,{"derivedFrom":makeQuery(id+"F5.opPattern","COPY",BODY,{"derivedFrom":makeQuery(id+"F4.opPattern","COPY",BODY,{"derivedFrom":makeQuery(id+"F3.opPattern","COPY",BODY,{"derivedFrom":makeQuery(id+"F2.opPattern","COPY",BODY,{"derivedFrom":makeQuery(id+"F1.opRevolve","SWEPT_BODY",BODY,{"disambiguationData":[OSD([sQuery(id+"F0.wireOp",EDGE,"E1")])]}),"instanceName":"1"}),"instanceName":"1"}),"instanceName":"1"}),"instanceName":"1"}),"instanceName":"1"}),"instanceName":"1"}),"instanceName":"1"}),"instanceName":"1"});
            var Q288;
            Q288=makeQuery(id+"F10.opPattern","COPY",BODY,{"derivedFrom":makeQuery(id+"F9.opPattern","COPY",BODY,{"derivedFrom":makeQuery(id+"F1.opRevolve","SWEPT_BODY",BODY,{"disambiguationData":[OSD([sQuery(id+"F0.wireOp",EDGE,"E1")])]}),"instanceName":"1"}),"instanceName":"1"});
            var Q289;
            Q289=makeQuery(id+"F10.opPattern","COPY",BODY,{"derivedFrom":makeQuery(id+"F9.opPattern","COPY",BODY,{"derivedFrom":makeQuery(id+"F2.opPattern","COPY",BODY,{"derivedFrom":makeQuery(id+"F1.opRevolve","SWEPT_BODY",BODY,{"disambiguationData":[OSD([sQuery(id+"F0.wireOp",EDGE,"E1")])]}),"instanceName":"1"}),"instanceName":"1"}),"instanceName":"1"});
            var Q290;
            Q290=makeQuery(id+"F10.opPattern","COPY",BODY,{"derivedFrom":makeQuery(id+"F9.opPattern","COPY",BODY,{"derivedFrom":makeQuery(id+"F3.opPattern","COPY",BODY,{"derivedFrom":makeQuery(id+"F2.opPattern","COPY",BODY,{"derivedFrom":makeQuery(id+"F1.opRevolve","SWEPT_BODY",BODY,{"disambiguationData":[OSD([sQuery(id+"F0.wireOp",EDGE,"E1")])]}),"instanceName":"1"}),"instanceName":"1"}),"instanceName":"1"}),"instanceName":"1"});
            var Q291;
            Q291=makeQuery(id+"F10.opPattern","COPY",BODY,{"derivedFrom":makeQuery(id+"F9.opPattern","COPY",BODY,{"derivedFrom":makeQuery(id+"F4.opPattern","COPY",BODY,{"derivedFrom":makeQuery(id+"F1.opRevolve","SWEPT_BODY",BODY,{"disambiguationData":[OSD([sQuery(id+"F0.wireOp",EDGE,"E1")])]}),"instanceName":"1"}),"instanceName":"1"}),"instanceName":"1"});
            var Q292;
            Q292=makeQuery(id+"F10.opPattern","COPY",BODY,{"derivedFrom":makeQuery(id+"F9.opPattern","COPY",BODY,{"derivedFrom":makeQuery(id+"F4.opPattern","COPY",BODY,{"derivedFrom":makeQuery(id+"F2.opPattern","COPY",BODY,{"derivedFrom":makeQuery(id+"F1.opRevolve","SWEPT_BODY",BODY,{"disambiguationData":[OSD([sQuery(id+"F0.wireOp",EDGE,"E1")])]}),"instanceName":"1"}),"instanceName":"1"}),"instanceName":"1"}),"instanceName":"1"});
            var Q293;
            Q293=makeQuery(id+"F10.opPattern","COPY",BODY,{"derivedFrom":makeQuery(id+"F9.opPattern","COPY",BODY,{"derivedFrom":makeQuery(id+"F4.opPattern","COPY",BODY,{"derivedFrom":makeQuery(id+"F3.opPattern","COPY",BODY,{"derivedFrom":makeQuery(id+"F2.opPattern","COPY",BODY,{"derivedFrom":makeQuery(id+"F1.opRevolve","SWEPT_BODY",BODY,{"disambiguationData":[OSD([sQuery(id+"F0.wireOp",EDGE,"E1")])]}),"instanceName":"1"}),"instanceName":"1"}),"instanceName":"1"}),"instanceName":"1"}),"instanceName":"1"});
            var Q294;
            Q294=makeQuery(id+"F10.opPattern","COPY",BODY,{"derivedFrom":makeQuery(id+"F9.opPattern","COPY",BODY,{"derivedFrom":makeQuery(id+"F5.opPattern","COPY",BODY,{"derivedFrom":makeQuery(id+"F1.opRevolve","SWEPT_BODY",BODY,{"disambiguationData":[OSD([sQuery(id+"F0.wireOp",EDGE,"E1")])]}),"instanceName":"1"}),"instanceName":"1"}),"instanceName":"1"});
            var Q295;
            Q295=makeQuery(id+"F10.opPattern","COPY",BODY,{"derivedFrom":makeQuery(id+"F9.opPattern","COPY",BODY,{"derivedFrom":makeQuery(id+"F5.opPattern","COPY",BODY,{"derivedFrom":makeQuery(id+"F2.opPattern","COPY",BODY,{"derivedFrom":makeQuery(id+"F1.opRevolve","SWEPT_BODY",BODY,{"disambiguationData":[OSD([sQuery(id+"F0.wireOp",EDGE,"E1")])]}),"instanceName":"1"}),"instanceName":"1"}),"instanceName":"1"}),"instanceName":"1"});
            var Q296;
            Q296=makeQuery(id+"F10.opPattern","COPY",BODY,{"derivedFrom":makeQuery(id+"F9.opPattern","COPY",BODY,{"derivedFrom":makeQuery(id+"F5.opPattern","COPY",BODY,{"derivedFrom":makeQuery(id+"F3.opPattern","COPY",BODY,{"derivedFrom":makeQuery(id+"F2.opPattern","COPY",BODY,{"derivedFrom":makeQuery(id+"F1.opRevolve","SWEPT_BODY",BODY,{"disambiguationData":[OSD([sQuery(id+"F0.wireOp",EDGE,"E1")])]}),"instanceName":"1"}),"instanceName":"1"}),"instanceName":"1"}),"instanceName":"1"}),"instanceName":"1"});
            var Q297;
            Q297=makeQuery(id+"F10.opPattern","COPY",BODY,{"derivedFrom":makeQuery(id+"F9.opPattern","COPY",BODY,{"derivedFrom":makeQuery(id+"F5.opPattern","COPY",BODY,{"derivedFrom":makeQuery(id+"F4.opPattern","COPY",BODY,{"derivedFrom":makeQuery(id+"F1.opRevolve","SWEPT_BODY",BODY,{"disambiguationData":[OSD([sQuery(id+"F0.wireOp",EDGE,"E1")])]}),"instanceName":"1"}),"instanceName":"1"}),"instanceName":"1"}),"instanceName":"1"});
            var Q298;
            Q298=makeQuery(id+"F10.opPattern","COPY",BODY,{"derivedFrom":makeQuery(id+"F9.opPattern","COPY",BODY,{"derivedFrom":makeQuery(id+"F5.opPattern","COPY",BODY,{"derivedFrom":makeQuery(id+"F4.opPattern","COPY",BODY,{"derivedFrom":makeQuery(id+"F2.opPattern","COPY",BODY,{"derivedFrom":makeQuery(id+"F1.opRevolve","SWEPT_BODY",BODY,{"disambiguationData":[OSD([sQuery(id+"F0.wireOp",EDGE,"E1")])]}),"instanceName":"1"}),"instanceName":"1"}),"instanceName":"1"}),"instanceName":"1"}),"instanceName":"1"});
            var Q299;
            Q299=makeQuery(id+"F10.opPattern","COPY",BODY,{"derivedFrom":makeQuery(id+"F9.opPattern","COPY",BODY,{"derivedFrom":makeQuery(id+"F5.opPattern","COPY",BODY,{"derivedFrom":makeQuery(id+"F4.opPattern","COPY",BODY,{"derivedFrom":makeQuery(id+"F3.opPattern","COPY",BODY,{"derivedFrom":makeQuery(id+"F2.opPattern","COPY",BODY,{"derivedFrom":makeQuery(id+"F1.opRevolve","SWEPT_BODY",BODY,{"disambiguationData":[OSD([sQuery(id+"F0.wireOp",EDGE,"E1")])]}),"instanceName":"1"}),"instanceName":"1"}),"instanceName":"1"}),"instanceName":"1"}),"instanceName":"1"}),"instanceName":"1"});
            var Q300;
            Q300=makeQuery(id+"F10.opPattern","COPY",BODY,{"derivedFrom":makeQuery(id+"F9.opPattern","COPY",BODY,{"derivedFrom":makeQuery(id+"F6.opPattern","COPY",BODY,{"derivedFrom":makeQuery(id+"F1.opRevolve","SWEPT_BODY",BODY,{"disambiguationData":[OSD([sQuery(id+"F0.wireOp",EDGE,"E1")])]}),"instanceName":"1"}),"instanceName":"1"}),"instanceName":"1"});
            var Q301;
            Q301=makeQuery(id+"F10.opPattern","COPY",BODY,{"derivedFrom":makeQuery(id+"F9.opPattern","COPY",BODY,{"derivedFrom":makeQuery(id+"F6.opPattern","COPY",BODY,{"derivedFrom":makeQuery(id+"F2.opPattern","COPY",BODY,{"derivedFrom":makeQuery(id+"F1.opRevolve","SWEPT_BODY",BODY,{"disambiguationData":[OSD([sQuery(id+"F0.wireOp",EDGE,"E1")])]}),"instanceName":"1"}),"instanceName":"1"}),"instanceName":"1"}),"instanceName":"1"});
            var Q302;
            Q302=makeQuery(id+"F10.opPattern","COPY",BODY,{"derivedFrom":makeQuery(id+"F9.opPattern","COPY",BODY,{"derivedFrom":makeQuery(id+"F6.opPattern","COPY",BODY,{"derivedFrom":makeQuery(id+"F3.opPattern","COPY",BODY,{"derivedFrom":makeQuery(id+"F2.opPattern","COPY",BODY,{"derivedFrom":makeQuery(id+"F1.opRevolve","SWEPT_BODY",BODY,{"disambiguationData":[OSD([sQuery(id+"F0.wireOp",EDGE,"E1")])]}),"instanceName":"1"}),"instanceName":"1"}),"instanceName":"1"}),"instanceName":"1"}),"instanceName":"1"});
            var Q303;
            Q303=makeQuery(id+"F10.opPattern","COPY",BODY,{"derivedFrom":makeQuery(id+"F9.opPattern","COPY",BODY,{"derivedFrom":makeQuery(id+"F6.opPattern","COPY",BODY,{"derivedFrom":makeQuery(id+"F4.opPattern","COPY",BODY,{"derivedFrom":makeQuery(id+"F1.opRevolve","SWEPT_BODY",BODY,{"disambiguationData":[OSD([sQuery(id+"F0.wireOp",EDGE,"E1")])]}),"instanceName":"1"}),"instanceName":"1"}),"instanceName":"1"}),"instanceName":"1"});
            var Q304;
            Q304=makeQuery(id+"F10.opPattern","COPY",BODY,{"derivedFrom":makeQuery(id+"F9.opPattern","COPY",BODY,{"derivedFrom":makeQuery(id+"F6.opPattern","COPY",BODY,{"derivedFrom":makeQuery(id+"F4.opPattern","COPY",BODY,{"derivedFrom":makeQuery(id+"F2.opPattern","COPY",BODY,{"derivedFrom":makeQuery(id+"F1.opRevolve","SWEPT_BODY",BODY,{"disambiguationData":[OSD([sQuery(id+"F0.wireOp",EDGE,"E1")])]}),"instanceName":"1"}),"instanceName":"1"}),"instanceName":"1"}),"instanceName":"1"}),"instanceName":"1"});
            var Q305;
            Q305=makeQuery(id+"F10.opPattern","COPY",BODY,{"derivedFrom":makeQuery(id+"F9.opPattern","COPY",BODY,{"derivedFrom":makeQuery(id+"F6.opPattern","COPY",BODY,{"derivedFrom":makeQuery(id+"F4.opPattern","COPY",BODY,{"derivedFrom":makeQuery(id+"F3.opPattern","COPY",BODY,{"derivedFrom":makeQuery(id+"F2.opPattern","COPY",BODY,{"derivedFrom":makeQuery(id+"F1.opRevolve","SWEPT_BODY",BODY,{"disambiguationData":[OSD([sQuery(id+"F0.wireOp",EDGE,"E1")])]}),"instanceName":"1"}),"instanceName":"1"}),"instanceName":"1"}),"instanceName":"1"}),"instanceName":"1"}),"instanceName":"1"});
            var Q306;
            Q306=makeQuery(id+"F10.opPattern","COPY",BODY,{"derivedFrom":makeQuery(id+"F9.opPattern","COPY",BODY,{"derivedFrom":makeQuery(id+"F6.opPattern","COPY",BODY,{"derivedFrom":makeQuery(id+"F5.opPattern","COPY",BODY,{"derivedFrom":makeQuery(id+"F1.opRevolve","SWEPT_BODY",BODY,{"disambiguationData":[OSD([sQuery(id+"F0.wireOp",EDGE,"E1")])]}),"instanceName":"1"}),"instanceName":"1"}),"instanceName":"1"}),"instanceName":"1"});
            var Q307;
            Q307=makeQuery(id+"F10.opPattern","COPY",BODY,{"derivedFrom":makeQuery(id+"F9.opPattern","COPY",BODY,{"derivedFrom":makeQuery(id+"F6.opPattern","COPY",BODY,{"derivedFrom":makeQuery(id+"F5.opPattern","COPY",BODY,{"derivedFrom":makeQuery(id+"F2.opPattern","COPY",BODY,{"derivedFrom":makeQuery(id+"F1.opRevolve","SWEPT_BODY",BODY,{"disambiguationData":[OSD([sQuery(id+"F0.wireOp",EDGE,"E1")])]}),"instanceName":"1"}),"instanceName":"1"}),"instanceName":"1"}),"instanceName":"1"}),"instanceName":"1"});
            var Q308;
            Q308=makeQuery(id+"F10.opPattern","COPY",BODY,{"derivedFrom":makeQuery(id+"F9.opPattern","COPY",BODY,{"derivedFrom":makeQuery(id+"F6.opPattern","COPY",BODY,{"derivedFrom":makeQuery(id+"F5.opPattern","COPY",BODY,{"derivedFrom":makeQuery(id+"F3.opPattern","COPY",BODY,{"derivedFrom":makeQuery(id+"F2.opPattern","COPY",BODY,{"derivedFrom":makeQuery(id+"F1.opRevolve","SWEPT_BODY",BODY,{"disambiguationData":[OSD([sQuery(id+"F0.wireOp",EDGE,"E1")])]}),"instanceName":"1"}),"instanceName":"1"}),"instanceName":"1"}),"instanceName":"1"}),"instanceName":"1"}),"instanceName":"1"});
            var Q309;
            Q309=makeQuery(id+"F10.opPattern","COPY",BODY,{"derivedFrom":makeQuery(id+"F9.opPattern","COPY",BODY,{"derivedFrom":makeQuery(id+"F6.opPattern","COPY",BODY,{"derivedFrom":makeQuery(id+"F5.opPattern","COPY",BODY,{"derivedFrom":makeQuery(id+"F4.opPattern","COPY",BODY,{"derivedFrom":makeQuery(id+"F1.opRevolve","SWEPT_BODY",BODY,{"disambiguationData":[OSD([sQuery(id+"F0.wireOp",EDGE,"E1")])]}),"instanceName":"1"}),"instanceName":"1"}),"instanceName":"1"}),"instanceName":"1"}),"instanceName":"1"});
            var Q310;
            Q310=makeQuery(id+"F10.opPattern","COPY",BODY,{"derivedFrom":makeQuery(id+"F9.opPattern","COPY",BODY,{"derivedFrom":makeQuery(id+"F6.opPattern","COPY",BODY,{"derivedFrom":makeQuery(id+"F5.opPattern","COPY",BODY,{"derivedFrom":makeQuery(id+"F4.opPattern","COPY",BODY,{"derivedFrom":makeQuery(id+"F2.opPattern","COPY",BODY,{"derivedFrom":makeQuery(id+"F1.opRevolve","SWEPT_BODY",BODY,{"disambiguationData":[OSD([sQuery(id+"F0.wireOp",EDGE,"E1")])]}),"instanceName":"1"}),"instanceName":"1"}),"instanceName":"1"}),"instanceName":"1"}),"instanceName":"1"}),"instanceName":"1"});
            var Q311;
            Q311=makeQuery(id+"F10.opPattern","COPY",BODY,{"derivedFrom":makeQuery(id+"F9.opPattern","COPY",BODY,{"derivedFrom":makeQuery(id+"F6.opPattern","COPY",BODY,{"derivedFrom":makeQuery(id+"F5.opPattern","COPY",BODY,{"derivedFrom":makeQuery(id+"F4.opPattern","COPY",BODY,{"derivedFrom":makeQuery(id+"F3.opPattern","COPY",BODY,{"derivedFrom":makeQuery(id+"F2.opPattern","COPY",BODY,{"derivedFrom":makeQuery(id+"F1.opRevolve","SWEPT_BODY",BODY,{"disambiguationData":[OSD([sQuery(id+"F0.wireOp",EDGE,"E1")])]}),"instanceName":"1"}),"instanceName":"1"}),"instanceName":"1"}),"instanceName":"1"}),"instanceName":"1"}),"instanceName":"1"}),"instanceName":"1"});
            var Q312;
            Q312=makeQuery(id+"F10.opPattern","COPY",BODY,{"derivedFrom":makeQuery(id+"F9.opPattern","COPY",BODY,{"derivedFrom":makeQuery(id+"F7.opPattern","COPY",BODY,{"derivedFrom":makeQuery(id+"F1.opRevolve","SWEPT_BODY",BODY,{"disambiguationData":[OSD([sQuery(id+"F0.wireOp",EDGE,"E1")])]}),"instanceName":"1"}),"instanceName":"1"}),"instanceName":"1"});
            var Q313;
            Q313=makeQuery(id+"F10.opPattern","COPY",BODY,{"derivedFrom":makeQuery(id+"F9.opPattern","COPY",BODY,{"derivedFrom":makeQuery(id+"F7.opPattern","COPY",BODY,{"derivedFrom":makeQuery(id+"F2.opPattern","COPY",BODY,{"derivedFrom":makeQuery(id+"F1.opRevolve","SWEPT_BODY",BODY,{"disambiguationData":[OSD([sQuery(id+"F0.wireOp",EDGE,"E1")])]}),"instanceName":"1"}),"instanceName":"1"}),"instanceName":"1"}),"instanceName":"1"});
            var Q314;
            Q314=makeQuery(id+"F10.opPattern","COPY",BODY,{"derivedFrom":makeQuery(id+"F9.opPattern","COPY",BODY,{"derivedFrom":makeQuery(id+"F7.opPattern","COPY",BODY,{"derivedFrom":makeQuery(id+"F3.opPattern","COPY",BODY,{"derivedFrom":makeQuery(id+"F2.opPattern","COPY",BODY,{"derivedFrom":makeQuery(id+"F1.opRevolve","SWEPT_BODY",BODY,{"disambiguationData":[OSD([sQuery(id+"F0.wireOp",EDGE,"E1")])]}),"instanceName":"1"}),"instanceName":"1"}),"instanceName":"1"}),"instanceName":"1"}),"instanceName":"1"});
            var Q315;
            Q315=makeQuery(id+"F10.opPattern","COPY",BODY,{"derivedFrom":makeQuery(id+"F9.opPattern","COPY",BODY,{"derivedFrom":makeQuery(id+"F7.opPattern","COPY",BODY,{"derivedFrom":makeQuery(id+"F4.opPattern","COPY",BODY,{"derivedFrom":makeQuery(id+"F1.opRevolve","SWEPT_BODY",BODY,{"disambiguationData":[OSD([sQuery(id+"F0.wireOp",EDGE,"E1")])]}),"instanceName":"1"}),"instanceName":"1"}),"instanceName":"1"}),"instanceName":"1"});
            var Q316;
            Q316=makeQuery(id+"F10.opPattern","COPY",BODY,{"derivedFrom":makeQuery(id+"F9.opPattern","COPY",BODY,{"derivedFrom":makeQuery(id+"F7.opPattern","COPY",BODY,{"derivedFrom":makeQuery(id+"F4.opPattern","COPY",BODY,{"derivedFrom":makeQuery(id+"F2.opPattern","COPY",BODY,{"derivedFrom":makeQuery(id+"F1.opRevolve","SWEPT_BODY",BODY,{"disambiguationData":[OSD([sQuery(id+"F0.wireOp",EDGE,"E1")])]}),"instanceName":"1"}),"instanceName":"1"}),"instanceName":"1"}),"instanceName":"1"}),"instanceName":"1"});
            var Q317;
            Q317=makeQuery(id+"F10.opPattern","COPY",BODY,{"derivedFrom":makeQuery(id+"F9.opPattern","COPY",BODY,{"derivedFrom":makeQuery(id+"F7.opPattern","COPY",BODY,{"derivedFrom":makeQuery(id+"F4.opPattern","COPY",BODY,{"derivedFrom":makeQuery(id+"F3.opPattern","COPY",BODY,{"derivedFrom":makeQuery(id+"F2.opPattern","COPY",BODY,{"derivedFrom":makeQuery(id+"F1.opRevolve","SWEPT_BODY",BODY,{"disambiguationData":[OSD([sQuery(id+"F0.wireOp",EDGE,"E1")])]}),"instanceName":"1"}),"instanceName":"1"}),"instanceName":"1"}),"instanceName":"1"}),"instanceName":"1"}),"instanceName":"1"});
            var Q318;
            Q318=makeQuery(id+"F10.opPattern","COPY",BODY,{"derivedFrom":makeQuery(id+"F9.opPattern","COPY",BODY,{"derivedFrom":makeQuery(id+"F7.opPattern","COPY",BODY,{"derivedFrom":makeQuery(id+"F5.opPattern","COPY",BODY,{"derivedFrom":makeQuery(id+"F1.opRevolve","SWEPT_BODY",BODY,{"disambiguationData":[OSD([sQuery(id+"F0.wireOp",EDGE,"E1")])]}),"instanceName":"1"}),"instanceName":"1"}),"instanceName":"1"}),"instanceName":"1"});
            var Q319;
            Q319=makeQuery(id+"F10.opPattern","COPY",BODY,{"derivedFrom":makeQuery(id+"F9.opPattern","COPY",BODY,{"derivedFrom":makeQuery(id+"F7.opPattern","COPY",BODY,{"derivedFrom":makeQuery(id+"F5.opPattern","COPY",BODY,{"derivedFrom":makeQuery(id+"F2.opPattern","COPY",BODY,{"derivedFrom":makeQuery(id+"F1.opRevolve","SWEPT_BODY",BODY,{"disambiguationData":[OSD([sQuery(id+"F0.wireOp",EDGE,"E1")])]}),"instanceName":"1"}),"instanceName":"1"}),"instanceName":"1"}),"instanceName":"1"}),"instanceName":"1"});
            var Q320;
            Q320=makeQuery(id+"F10.opPattern","COPY",BODY,{"derivedFrom":makeQuery(id+"F9.opPattern","COPY",BODY,{"derivedFrom":makeQuery(id+"F7.opPattern","COPY",BODY,{"derivedFrom":makeQuery(id+"F5.opPattern","COPY",BODY,{"derivedFrom":makeQuery(id+"F3.opPattern","COPY",BODY,{"derivedFrom":makeQuery(id+"F2.opPattern","COPY",BODY,{"derivedFrom":makeQuery(id+"F1.opRevolve","SWEPT_BODY",BODY,{"disambiguationData":[OSD([sQuery(id+"F0.wireOp",EDGE,"E1")])]}),"instanceName":"1"}),"instanceName":"1"}),"instanceName":"1"}),"instanceName":"1"}),"instanceName":"1"}),"instanceName":"1"});
            var Q321;
            Q321=makeQuery(id+"F10.opPattern","COPY",BODY,{"derivedFrom":makeQuery(id+"F9.opPattern","COPY",BODY,{"derivedFrom":makeQuery(id+"F7.opPattern","COPY",BODY,{"derivedFrom":makeQuery(id+"F5.opPattern","COPY",BODY,{"derivedFrom":makeQuery(id+"F4.opPattern","COPY",BODY,{"derivedFrom":makeQuery(id+"F1.opRevolve","SWEPT_BODY",BODY,{"disambiguationData":[OSD([sQuery(id+"F0.wireOp",EDGE,"E1")])]}),"instanceName":"1"}),"instanceName":"1"}),"instanceName":"1"}),"instanceName":"1"}),"instanceName":"1"});
            var Q322;
            Q322=makeQuery(id+"F10.opPattern","COPY",BODY,{"derivedFrom":makeQuery(id+"F9.opPattern","COPY",BODY,{"derivedFrom":makeQuery(id+"F7.opPattern","COPY",BODY,{"derivedFrom":makeQuery(id+"F5.opPattern","COPY",BODY,{"derivedFrom":makeQuery(id+"F4.opPattern","COPY",BODY,{"derivedFrom":makeQuery(id+"F2.opPattern","COPY",BODY,{"derivedFrom":makeQuery(id+"F1.opRevolve","SWEPT_BODY",BODY,{"disambiguationData":[OSD([sQuery(id+"F0.wireOp",EDGE,"E1")])]}),"instanceName":"1"}),"instanceName":"1"}),"instanceName":"1"}),"instanceName":"1"}),"instanceName":"1"}),"instanceName":"1"});
            var Q323;
            Q323=makeQuery(id+"F10.opPattern","COPY",BODY,{"derivedFrom":makeQuery(id+"F9.opPattern","COPY",BODY,{"derivedFrom":makeQuery(id+"F7.opPattern","COPY",BODY,{"derivedFrom":makeQuery(id+"F5.opPattern","COPY",BODY,{"derivedFrom":makeQuery(id+"F4.opPattern","COPY",BODY,{"derivedFrom":makeQuery(id+"F3.opPattern","COPY",BODY,{"derivedFrom":makeQuery(id+"F2.opPattern","COPY",BODY,{"derivedFrom":makeQuery(id+"F1.opRevolve","SWEPT_BODY",BODY,{"disambiguationData":[OSD([sQuery(id+"F0.wireOp",EDGE,"E1")])]}),"instanceName":"1"}),"instanceName":"1"}),"instanceName":"1"}),"instanceName":"1"}),"instanceName":"1"}),"instanceName":"1"}),"instanceName":"1"});
            var Q324;
            Q324=makeQuery(id+"F10.opPattern","COPY",BODY,{"derivedFrom":makeQuery(id+"F9.opPattern","COPY",BODY,{"derivedFrom":makeQuery(id+"F7.opPattern","COPY",BODY,{"derivedFrom":makeQuery(id+"F6.opPattern","COPY",BODY,{"derivedFrom":makeQuery(id+"F1.opRevolve","SWEPT_BODY",BODY,{"disambiguationData":[OSD([sQuery(id+"F0.wireOp",EDGE,"E1")])]}),"instanceName":"1"}),"instanceName":"1"}),"instanceName":"1"}),"instanceName":"1"});
            var Q325;
            Q325=makeQuery(id+"F10.opPattern","COPY",BODY,{"derivedFrom":makeQuery(id+"F9.opPattern","COPY",BODY,{"derivedFrom":makeQuery(id+"F7.opPattern","COPY",BODY,{"derivedFrom":makeQuery(id+"F6.opPattern","COPY",BODY,{"derivedFrom":makeQuery(id+"F2.opPattern","COPY",BODY,{"derivedFrom":makeQuery(id+"F1.opRevolve","SWEPT_BODY",BODY,{"disambiguationData":[OSD([sQuery(id+"F0.wireOp",EDGE,"E1")])]}),"instanceName":"1"}),"instanceName":"1"}),"instanceName":"1"}),"instanceName":"1"}),"instanceName":"1"});
            var Q326;
            Q326=makeQuery(id+"F10.opPattern","COPY",BODY,{"derivedFrom":makeQuery(id+"F9.opPattern","COPY",BODY,{"derivedFrom":makeQuery(id+"F7.opPattern","COPY",BODY,{"derivedFrom":makeQuery(id+"F6.opPattern","COPY",BODY,{"derivedFrom":makeQuery(id+"F3.opPattern","COPY",BODY,{"derivedFrom":makeQuery(id+"F2.opPattern","COPY",BODY,{"derivedFrom":makeQuery(id+"F1.opRevolve","SWEPT_BODY",BODY,{"disambiguationData":[OSD([sQuery(id+"F0.wireOp",EDGE,"E1")])]}),"instanceName":"1"}),"instanceName":"1"}),"instanceName":"1"}),"instanceName":"1"}),"instanceName":"1"}),"instanceName":"1"});
            var Q327;
            Q327=makeQuery(id+"F10.opPattern","COPY",BODY,{"derivedFrom":makeQuery(id+"F9.opPattern","COPY",BODY,{"derivedFrom":makeQuery(id+"F7.opPattern","COPY",BODY,{"derivedFrom":makeQuery(id+"F6.opPattern","COPY",BODY,{"derivedFrom":makeQuery(id+"F4.opPattern","COPY",BODY,{"derivedFrom":makeQuery(id+"F1.opRevolve","SWEPT_BODY",BODY,{"disambiguationData":[OSD([sQuery(id+"F0.wireOp",EDGE,"E1")])]}),"instanceName":"1"}),"instanceName":"1"}),"instanceName":"1"}),"instanceName":"1"}),"instanceName":"1"});
            var Q328;
            Q328=makeQuery(id+"F10.opPattern","COPY",BODY,{"derivedFrom":makeQuery(id+"F9.opPattern","COPY",BODY,{"derivedFrom":makeQuery(id+"F7.opPattern","COPY",BODY,{"derivedFrom":makeQuery(id+"F6.opPattern","COPY",BODY,{"derivedFrom":makeQuery(id+"F4.opPattern","COPY",BODY,{"derivedFrom":makeQuery(id+"F2.opPattern","COPY",BODY,{"derivedFrom":makeQuery(id+"F1.opRevolve","SWEPT_BODY",BODY,{"disambiguationData":[OSD([sQuery(id+"F0.wireOp",EDGE,"E1")])]}),"instanceName":"1"}),"instanceName":"1"}),"instanceName":"1"}),"instanceName":"1"}),"instanceName":"1"}),"instanceName":"1"});
            var Q329;
            Q329=makeQuery(id+"F10.opPattern","COPY",BODY,{"derivedFrom":makeQuery(id+"F9.opPattern","COPY",BODY,{"derivedFrom":makeQuery(id+"F7.opPattern","COPY",BODY,{"derivedFrom":makeQuery(id+"F6.opPattern","COPY",BODY,{"derivedFrom":makeQuery(id+"F4.opPattern","COPY",BODY,{"derivedFrom":makeQuery(id+"F3.opPattern","COPY",BODY,{"derivedFrom":makeQuery(id+"F2.opPattern","COPY",BODY,{"derivedFrom":makeQuery(id+"F1.opRevolve","SWEPT_BODY",BODY,{"disambiguationData":[OSD([sQuery(id+"F0.wireOp",EDGE,"E1")])]}),"instanceName":"1"}),"instanceName":"1"}),"instanceName":"1"}),"instanceName":"1"}),"instanceName":"1"}),"instanceName":"1"}),"instanceName":"1"});
            var Q330;
            Q330=makeQuery(id+"F10.opPattern","COPY",BODY,{"derivedFrom":makeQuery(id+"F9.opPattern","COPY",BODY,{"derivedFrom":makeQuery(id+"F7.opPattern","COPY",BODY,{"derivedFrom":makeQuery(id+"F6.opPattern","COPY",BODY,{"derivedFrom":makeQuery(id+"F5.opPattern","COPY",BODY,{"derivedFrom":makeQuery(id+"F1.opRevolve","SWEPT_BODY",BODY,{"disambiguationData":[OSD([sQuery(id+"F0.wireOp",EDGE,"E1")])]}),"instanceName":"1"}),"instanceName":"1"}),"instanceName":"1"}),"instanceName":"1"}),"instanceName":"1"});
            var Q331;
            Q331=makeQuery(id+"F10.opPattern","COPY",BODY,{"derivedFrom":makeQuery(id+"F9.opPattern","COPY",BODY,{"derivedFrom":makeQuery(id+"F7.opPattern","COPY",BODY,{"derivedFrom":makeQuery(id+"F6.opPattern","COPY",BODY,{"derivedFrom":makeQuery(id+"F5.opPattern","COPY",BODY,{"derivedFrom":makeQuery(id+"F2.opPattern","COPY",BODY,{"derivedFrom":makeQuery(id+"F1.opRevolve","SWEPT_BODY",BODY,{"disambiguationData":[OSD([sQuery(id+"F0.wireOp",EDGE,"E1")])]}),"instanceName":"1"}),"instanceName":"1"}),"instanceName":"1"}),"instanceName":"1"}),"instanceName":"1"}),"instanceName":"1"});
            var Q332;
            Q332=makeQuery(id+"F10.opPattern","COPY",BODY,{"derivedFrom":makeQuery(id+"F9.opPattern","COPY",BODY,{"derivedFrom":makeQuery(id+"F7.opPattern","COPY",BODY,{"derivedFrom":makeQuery(id+"F6.opPattern","COPY",BODY,{"derivedFrom":makeQuery(id+"F5.opPattern","COPY",BODY,{"derivedFrom":makeQuery(id+"F3.opPattern","COPY",BODY,{"derivedFrom":makeQuery(id+"F2.opPattern","COPY",BODY,{"derivedFrom":makeQuery(id+"F1.opRevolve","SWEPT_BODY",BODY,{"disambiguationData":[OSD([sQuery(id+"F0.wireOp",EDGE,"E1")])]}),"instanceName":"1"}),"instanceName":"1"}),"instanceName":"1"}),"instanceName":"1"}),"instanceName":"1"}),"instanceName":"1"}),"instanceName":"1"});
            var Q333;
            Q333=makeQuery(id+"F10.opPattern","COPY",BODY,{"derivedFrom":makeQuery(id+"F9.opPattern","COPY",BODY,{"derivedFrom":makeQuery(id+"F7.opPattern","COPY",BODY,{"derivedFrom":makeQuery(id+"F6.opPattern","COPY",BODY,{"derivedFrom":makeQuery(id+"F5.opPattern","COPY",BODY,{"derivedFrom":makeQuery(id+"F4.opPattern","COPY",BODY,{"derivedFrom":makeQuery(id+"F1.opRevolve","SWEPT_BODY",BODY,{"disambiguationData":[OSD([sQuery(id+"F0.wireOp",EDGE,"E1")])]}),"instanceName":"1"}),"instanceName":"1"}),"instanceName":"1"}),"instanceName":"1"}),"instanceName":"1"}),"instanceName":"1"});
            var Q334;
            Q334=makeQuery(id+"F10.opPattern","COPY",BODY,{"derivedFrom":makeQuery(id+"F9.opPattern","COPY",BODY,{"derivedFrom":makeQuery(id+"F7.opPattern","COPY",BODY,{"derivedFrom":makeQuery(id+"F6.opPattern","COPY",BODY,{"derivedFrom":makeQuery(id+"F5.opPattern","COPY",BODY,{"derivedFrom":makeQuery(id+"F4.opPattern","COPY",BODY,{"derivedFrom":makeQuery(id+"F2.opPattern","COPY",BODY,{"derivedFrom":makeQuery(id+"F1.opRevolve","SWEPT_BODY",BODY,{"disambiguationData":[OSD([sQuery(id+"F0.wireOp",EDGE,"E1")])]}),"instanceName":"1"}),"instanceName":"1"}),"instanceName":"1"}),"instanceName":"1"}),"instanceName":"1"}),"instanceName":"1"}),"instanceName":"1"});
            var Q335;
            Q335=makeQuery(id+"F10.opPattern","COPY",BODY,{"derivedFrom":makeQuery(id+"F9.opPattern","COPY",BODY,{"derivedFrom":makeQuery(id+"F7.opPattern","COPY",BODY,{"derivedFrom":makeQuery(id+"F6.opPattern","COPY",BODY,{"derivedFrom":makeQuery(id+"F5.opPattern","COPY",BODY,{"derivedFrom":makeQuery(id+"F4.opPattern","COPY",BODY,{"derivedFrom":makeQuery(id+"F3.opPattern","COPY",BODY,{"derivedFrom":makeQuery(id+"F2.opPattern","COPY",BODY,{"derivedFrom":makeQuery(id+"F1.opRevolve","SWEPT_BODY",BODY,{"disambiguationData":[OSD([sQuery(id+"F0.wireOp",EDGE,"E1")])]}),"instanceName":"1"}),"instanceName":"1"}),"instanceName":"1"}),"instanceName":"1"}),"instanceName":"1"}),"instanceName":"1"}),"instanceName":"1"}),"instanceName":"1"});
            var Q336;
            Q336=makeQuery(id+"F10.opPattern","COPY",BODY,{"derivedFrom":makeQuery(id+"F9.opPattern","COPY",BODY,{"derivedFrom":makeQuery(id+"F8.opPattern","COPY",BODY,{"derivedFrom":makeQuery(id+"F1.opRevolve","SWEPT_BODY",BODY,{"disambiguationData":[OSD([sQuery(id+"F0.wireOp",EDGE,"E1")])]}),"instanceName":"1"}),"instanceName":"1"}),"instanceName":"1"});
            var Q337;
            Q337=makeQuery(id+"F10.opPattern","COPY",BODY,{"derivedFrom":makeQuery(id+"F9.opPattern","COPY",BODY,{"derivedFrom":makeQuery(id+"F8.opPattern","COPY",BODY,{"derivedFrom":makeQuery(id+"F2.opPattern","COPY",BODY,{"derivedFrom":makeQuery(id+"F1.opRevolve","SWEPT_BODY",BODY,{"disambiguationData":[OSD([sQuery(id+"F0.wireOp",EDGE,"E1")])]}),"instanceName":"1"}),"instanceName":"1"}),"instanceName":"1"}),"instanceName":"1"});
            var Q338;
            Q338=makeQuery(id+"F10.opPattern","COPY",BODY,{"derivedFrom":makeQuery(id+"F9.opPattern","COPY",BODY,{"derivedFrom":makeQuery(id+"F8.opPattern","COPY",BODY,{"derivedFrom":makeQuery(id+"F3.opPattern","COPY",BODY,{"derivedFrom":makeQuery(id+"F2.opPattern","COPY",BODY,{"derivedFrom":makeQuery(id+"F1.opRevolve","SWEPT_BODY",BODY,{"disambiguationData":[OSD([sQuery(id+"F0.wireOp",EDGE,"E1")])]}),"instanceName":"1"}),"instanceName":"1"}),"instanceName":"1"}),"instanceName":"1"}),"instanceName":"1"});
            var Q339;
            Q339=makeQuery(id+"F10.opPattern","COPY",BODY,{"derivedFrom":makeQuery(id+"F9.opPattern","COPY",BODY,{"derivedFrom":makeQuery(id+"F8.opPattern","COPY",BODY,{"derivedFrom":makeQuery(id+"F4.opPattern","COPY",BODY,{"derivedFrom":makeQuery(id+"F1.opRevolve","SWEPT_BODY",BODY,{"disambiguationData":[OSD([sQuery(id+"F0.wireOp",EDGE,"E1")])]}),"instanceName":"1"}),"instanceName":"1"}),"instanceName":"1"}),"instanceName":"1"});
            var Q340;
            Q340=makeQuery(id+"F10.opPattern","COPY",BODY,{"derivedFrom":makeQuery(id+"F9.opPattern","COPY",BODY,{"derivedFrom":makeQuery(id+"F8.opPattern","COPY",BODY,{"derivedFrom":makeQuery(id+"F4.opPattern","COPY",BODY,{"derivedFrom":makeQuery(id+"F2.opPattern","COPY",BODY,{"derivedFrom":makeQuery(id+"F1.opRevolve","SWEPT_BODY",BODY,{"disambiguationData":[OSD([sQuery(id+"F0.wireOp",EDGE,"E1")])]}),"instanceName":"1"}),"instanceName":"1"}),"instanceName":"1"}),"instanceName":"1"}),"instanceName":"1"});
            var Q341;
            Q341=makeQuery(id+"F10.opPattern","COPY",BODY,{"derivedFrom":makeQuery(id+"F9.opPattern","COPY",BODY,{"derivedFrom":makeQuery(id+"F8.opPattern","COPY",BODY,{"derivedFrom":makeQuery(id+"F4.opPattern","COPY",BODY,{"derivedFrom":makeQuery(id+"F3.opPattern","COPY",BODY,{"derivedFrom":makeQuery(id+"F2.opPattern","COPY",BODY,{"derivedFrom":makeQuery(id+"F1.opRevolve","SWEPT_BODY",BODY,{"disambiguationData":[OSD([sQuery(id+"F0.wireOp",EDGE,"E1")])]}),"instanceName":"1"}),"instanceName":"1"}),"instanceName":"1"}),"instanceName":"1"}),"instanceName":"1"}),"instanceName":"1"});
            var Q342;
            Q342=makeQuery(id+"F10.opPattern","COPY",BODY,{"derivedFrom":makeQuery(id+"F9.opPattern","COPY",BODY,{"derivedFrom":makeQuery(id+"F8.opPattern","COPY",BODY,{"derivedFrom":makeQuery(id+"F5.opPattern","COPY",BODY,{"derivedFrom":makeQuery(id+"F1.opRevolve","SWEPT_BODY",BODY,{"disambiguationData":[OSD([sQuery(id+"F0.wireOp",EDGE,"E1")])]}),"instanceName":"1"}),"instanceName":"1"}),"instanceName":"1"}),"instanceName":"1"});
            var Q343;
            Q343=makeQuery(id+"F10.opPattern","COPY",BODY,{"derivedFrom":makeQuery(id+"F9.opPattern","COPY",BODY,{"derivedFrom":makeQuery(id+"F8.opPattern","COPY",BODY,{"derivedFrom":makeQuery(id+"F5.opPattern","COPY",BODY,{"derivedFrom":makeQuery(id+"F2.opPattern","COPY",BODY,{"derivedFrom":makeQuery(id+"F1.opRevolve","SWEPT_BODY",BODY,{"disambiguationData":[OSD([sQuery(id+"F0.wireOp",EDGE,"E1")])]}),"instanceName":"1"}),"instanceName":"1"}),"instanceName":"1"}),"instanceName":"1"}),"instanceName":"1"});
            var Q344;
            Q344=makeQuery(id+"F10.opPattern","COPY",BODY,{"derivedFrom":makeQuery(id+"F9.opPattern","COPY",BODY,{"derivedFrom":makeQuery(id+"F8.opPattern","COPY",BODY,{"derivedFrom":makeQuery(id+"F5.opPattern","COPY",BODY,{"derivedFrom":makeQuery(id+"F3.opPattern","COPY",BODY,{"derivedFrom":makeQuery(id+"F2.opPattern","COPY",BODY,{"derivedFrom":makeQuery(id+"F1.opRevolve","SWEPT_BODY",BODY,{"disambiguationData":[OSD([sQuery(id+"F0.wireOp",EDGE,"E1")])]}),"instanceName":"1"}),"instanceName":"1"}),"instanceName":"1"}),"instanceName":"1"}),"instanceName":"1"}),"instanceName":"1"});
            var Q345;
            Q345=makeQuery(id+"F10.opPattern","COPY",BODY,{"derivedFrom":makeQuery(id+"F9.opPattern","COPY",BODY,{"derivedFrom":makeQuery(id+"F8.opPattern","COPY",BODY,{"derivedFrom":makeQuery(id+"F5.opPattern","COPY",BODY,{"derivedFrom":makeQuery(id+"F4.opPattern","COPY",BODY,{"derivedFrom":makeQuery(id+"F1.opRevolve","SWEPT_BODY",BODY,{"disambiguationData":[OSD([sQuery(id+"F0.wireOp",EDGE,"E1")])]}),"instanceName":"1"}),"instanceName":"1"}),"instanceName":"1"}),"instanceName":"1"}),"instanceName":"1"});
            var Q346;
            Q346=makeQuery(id+"F10.opPattern","COPY",BODY,{"derivedFrom":makeQuery(id+"F9.opPattern","COPY",BODY,{"derivedFrom":makeQuery(id+"F8.opPattern","COPY",BODY,{"derivedFrom":makeQuery(id+"F5.opPattern","COPY",BODY,{"derivedFrom":makeQuery(id+"F4.opPattern","COPY",BODY,{"derivedFrom":makeQuery(id+"F2.opPattern","COPY",BODY,{"derivedFrom":makeQuery(id+"F1.opRevolve","SWEPT_BODY",BODY,{"disambiguationData":[OSD([sQuery(id+"F0.wireOp",EDGE,"E1")])]}),"instanceName":"1"}),"instanceName":"1"}),"instanceName":"1"}),"instanceName":"1"}),"instanceName":"1"}),"instanceName":"1"});
            var Q347;
            Q347=makeQuery(id+"F10.opPattern","COPY",BODY,{"derivedFrom":makeQuery(id+"F9.opPattern","COPY",BODY,{"derivedFrom":makeQuery(id+"F8.opPattern","COPY",BODY,{"derivedFrom":makeQuery(id+"F5.opPattern","COPY",BODY,{"derivedFrom":makeQuery(id+"F4.opPattern","COPY",BODY,{"derivedFrom":makeQuery(id+"F3.opPattern","COPY",BODY,{"derivedFrom":makeQuery(id+"F2.opPattern","COPY",BODY,{"derivedFrom":makeQuery(id+"F1.opRevolve","SWEPT_BODY",BODY,{"disambiguationData":[OSD([sQuery(id+"F0.wireOp",EDGE,"E1")])]}),"instanceName":"1"}),"instanceName":"1"}),"instanceName":"1"}),"instanceName":"1"}),"instanceName":"1"}),"instanceName":"1"}),"instanceName":"1"});
            var Q348;
            Q348=makeQuery(id+"F10.opPattern","COPY",BODY,{"derivedFrom":makeQuery(id+"F9.opPattern","COPY",BODY,{"derivedFrom":makeQuery(id+"F8.opPattern","COPY",BODY,{"derivedFrom":makeQuery(id+"F6.opPattern","COPY",BODY,{"derivedFrom":makeQuery(id+"F1.opRevolve","SWEPT_BODY",BODY,{"disambiguationData":[OSD([sQuery(id+"F0.wireOp",EDGE,"E1")])]}),"instanceName":"1"}),"instanceName":"1"}),"instanceName":"1"}),"instanceName":"1"});
            var Q349;
            Q349=makeQuery(id+"F10.opPattern","COPY",BODY,{"derivedFrom":makeQuery(id+"F9.opPattern","COPY",BODY,{"derivedFrom":makeQuery(id+"F8.opPattern","COPY",BODY,{"derivedFrom":makeQuery(id+"F6.opPattern","COPY",BODY,{"derivedFrom":makeQuery(id+"F2.opPattern","COPY",BODY,{"derivedFrom":makeQuery(id+"F1.opRevolve","SWEPT_BODY",BODY,{"disambiguationData":[OSD([sQuery(id+"F0.wireOp",EDGE,"E1")])]}),"instanceName":"1"}),"instanceName":"1"}),"instanceName":"1"}),"instanceName":"1"}),"instanceName":"1"});
            var Q350;
            Q350=makeQuery(id+"F10.opPattern","COPY",BODY,{"derivedFrom":makeQuery(id+"F9.opPattern","COPY",BODY,{"derivedFrom":makeQuery(id+"F8.opPattern","COPY",BODY,{"derivedFrom":makeQuery(id+"F6.opPattern","COPY",BODY,{"derivedFrom":makeQuery(id+"F3.opPattern","COPY",BODY,{"derivedFrom":makeQuery(id+"F2.opPattern","COPY",BODY,{"derivedFrom":makeQuery(id+"F1.opRevolve","SWEPT_BODY",BODY,{"disambiguationData":[OSD([sQuery(id+"F0.wireOp",EDGE,"E1")])]}),"instanceName":"1"}),"instanceName":"1"}),"instanceName":"1"}),"instanceName":"1"}),"instanceName":"1"}),"instanceName":"1"});
            var Q351;
            Q351=makeQuery(id+"F10.opPattern","COPY",BODY,{"derivedFrom":makeQuery(id+"F9.opPattern","COPY",BODY,{"derivedFrom":makeQuery(id+"F8.opPattern","COPY",BODY,{"derivedFrom":makeQuery(id+"F6.opPattern","COPY",BODY,{"derivedFrom":makeQuery(id+"F4.opPattern","COPY",BODY,{"derivedFrom":makeQuery(id+"F1.opRevolve","SWEPT_BODY",BODY,{"disambiguationData":[OSD([sQuery(id+"F0.wireOp",EDGE,"E1")])]}),"instanceName":"1"}),"instanceName":"1"}),"instanceName":"1"}),"instanceName":"1"}),"instanceName":"1"});
            var Q352;
            Q352=makeQuery(id+"F10.opPattern","COPY",BODY,{"derivedFrom":makeQuery(id+"F9.opPattern","COPY",BODY,{"derivedFrom":makeQuery(id+"F8.opPattern","COPY",BODY,{"derivedFrom":makeQuery(id+"F6.opPattern","COPY",BODY,{"derivedFrom":makeQuery(id+"F4.opPattern","COPY",BODY,{"derivedFrom":makeQuery(id+"F2.opPattern","COPY",BODY,{"derivedFrom":makeQuery(id+"F1.opRevolve","SWEPT_BODY",BODY,{"disambiguationData":[OSD([sQuery(id+"F0.wireOp",EDGE,"E1")])]}),"instanceName":"1"}),"instanceName":"1"}),"instanceName":"1"}),"instanceName":"1"}),"instanceName":"1"}),"instanceName":"1"});
            var Q353;
            Q353=makeQuery(id+"F10.opPattern","COPY",BODY,{"derivedFrom":makeQuery(id+"F9.opPattern","COPY",BODY,{"derivedFrom":makeQuery(id+"F8.opPattern","COPY",BODY,{"derivedFrom":makeQuery(id+"F6.opPattern","COPY",BODY,{"derivedFrom":makeQuery(id+"F4.opPattern","COPY",BODY,{"derivedFrom":makeQuery(id+"F3.opPattern","COPY",BODY,{"derivedFrom":makeQuery(id+"F2.opPattern","COPY",BODY,{"derivedFrom":makeQuery(id+"F1.opRevolve","SWEPT_BODY",BODY,{"disambiguationData":[OSD([sQuery(id+"F0.wireOp",EDGE,"E1")])]}),"instanceName":"1"}),"instanceName":"1"}),"instanceName":"1"}),"instanceName":"1"}),"instanceName":"1"}),"instanceName":"1"}),"instanceName":"1"});
            var Q354;
            Q354=makeQuery(id+"F10.opPattern","COPY",BODY,{"derivedFrom":makeQuery(id+"F9.opPattern","COPY",BODY,{"derivedFrom":makeQuery(id+"F8.opPattern","COPY",BODY,{"derivedFrom":makeQuery(id+"F6.opPattern","COPY",BODY,{"derivedFrom":makeQuery(id+"F5.opPattern","COPY",BODY,{"derivedFrom":makeQuery(id+"F1.opRevolve","SWEPT_BODY",BODY,{"disambiguationData":[OSD([sQuery(id+"F0.wireOp",EDGE,"E1")])]}),"instanceName":"1"}),"instanceName":"1"}),"instanceName":"1"}),"instanceName":"1"}),"instanceName":"1"});
            var Q355;
            Q355=makeQuery(id+"F10.opPattern","COPY",BODY,{"derivedFrom":makeQuery(id+"F9.opPattern","COPY",BODY,{"derivedFrom":makeQuery(id+"F8.opPattern","COPY",BODY,{"derivedFrom":makeQuery(id+"F6.opPattern","COPY",BODY,{"derivedFrom":makeQuery(id+"F5.opPattern","COPY",BODY,{"derivedFrom":makeQuery(id+"F2.opPattern","COPY",BODY,{"derivedFrom":makeQuery(id+"F1.opRevolve","SWEPT_BODY",BODY,{"disambiguationData":[OSD([sQuery(id+"F0.wireOp",EDGE,"E1")])]}),"instanceName":"1"}),"instanceName":"1"}),"instanceName":"1"}),"instanceName":"1"}),"instanceName":"1"}),"instanceName":"1"});
            var Q356;
            Q356=makeQuery(id+"F10.opPattern","COPY",BODY,{"derivedFrom":makeQuery(id+"F9.opPattern","COPY",BODY,{"derivedFrom":makeQuery(id+"F8.opPattern","COPY",BODY,{"derivedFrom":makeQuery(id+"F6.opPattern","COPY",BODY,{"derivedFrom":makeQuery(id+"F5.opPattern","COPY",BODY,{"derivedFrom":makeQuery(id+"F3.opPattern","COPY",BODY,{"derivedFrom":makeQuery(id+"F2.opPattern","COPY",BODY,{"derivedFrom":makeQuery(id+"F1.opRevolve","SWEPT_BODY",BODY,{"disambiguationData":[OSD([sQuery(id+"F0.wireOp",EDGE,"E1")])]}),"instanceName":"1"}),"instanceName":"1"}),"instanceName":"1"}),"instanceName":"1"}),"instanceName":"1"}),"instanceName":"1"}),"instanceName":"1"});
            var Q357;
            Q357=makeQuery(id+"F10.opPattern","COPY",BODY,{"derivedFrom":makeQuery(id+"F9.opPattern","COPY",BODY,{"derivedFrom":makeQuery(id+"F8.opPattern","COPY",BODY,{"derivedFrom":makeQuery(id+"F6.opPattern","COPY",BODY,{"derivedFrom":makeQuery(id+"F5.opPattern","COPY",BODY,{"derivedFrom":makeQuery(id+"F4.opPattern","COPY",BODY,{"derivedFrom":makeQuery(id+"F1.opRevolve","SWEPT_BODY",BODY,{"disambiguationData":[OSD([sQuery(id+"F0.wireOp",EDGE,"E1")])]}),"instanceName":"1"}),"instanceName":"1"}),"instanceName":"1"}),"instanceName":"1"}),"instanceName":"1"}),"instanceName":"1"});
            var Q358;
            Q358=makeQuery(id+"F10.opPattern","COPY",BODY,{"derivedFrom":makeQuery(id+"F9.opPattern","COPY",BODY,{"derivedFrom":makeQuery(id+"F8.opPattern","COPY",BODY,{"derivedFrom":makeQuery(id+"F6.opPattern","COPY",BODY,{"derivedFrom":makeQuery(id+"F5.opPattern","COPY",BODY,{"derivedFrom":makeQuery(id+"F4.opPattern","COPY",BODY,{"derivedFrom":makeQuery(id+"F2.opPattern","COPY",BODY,{"derivedFrom":makeQuery(id+"F1.opRevolve","SWEPT_BODY",BODY,{"disambiguationData":[OSD([sQuery(id+"F0.wireOp",EDGE,"E1")])]}),"instanceName":"1"}),"instanceName":"1"}),"instanceName":"1"}),"instanceName":"1"}),"instanceName":"1"}),"instanceName":"1"}),"instanceName":"1"});
            var Q359;
            Q359=makeQuery(id+"F10.opPattern","COPY",BODY,{"derivedFrom":makeQuery(id+"F9.opPattern","COPY",BODY,{"derivedFrom":makeQuery(id+"F8.opPattern","COPY",BODY,{"derivedFrom":makeQuery(id+"F6.opPattern","COPY",BODY,{"derivedFrom":makeQuery(id+"F5.opPattern","COPY",BODY,{"derivedFrom":makeQuery(id+"F4.opPattern","COPY",BODY,{"derivedFrom":makeQuery(id+"F3.opPattern","COPY",BODY,{"derivedFrom":makeQuery(id+"F2.opPattern","COPY",BODY,{"derivedFrom":makeQuery(id+"F1.opRevolve","SWEPT_BODY",BODY,{"disambiguationData":[OSD([sQuery(id+"F0.wireOp",EDGE,"E1")])]}),"instanceName":"1"}),"instanceName":"1"}),"instanceName":"1"}),"instanceName":"1"}),"instanceName":"1"}),"instanceName":"1"}),"instanceName":"1"}),"instanceName":"1"});
            var Q360;
            Q360=makeQuery(id+"F10.opPattern","COPY",BODY,{"derivedFrom":makeQuery(id+"F9.opPattern","COPY",BODY,{"derivedFrom":makeQuery(id+"F8.opPattern","COPY",BODY,{"derivedFrom":makeQuery(id+"F7.opPattern","COPY",BODY,{"derivedFrom":makeQuery(id+"F1.opRevolve","SWEPT_BODY",BODY,{"disambiguationData":[OSD([sQuery(id+"F0.wireOp",EDGE,"E1")])]}),"instanceName":"1"}),"instanceName":"1"}),"instanceName":"1"}),"instanceName":"1"});
            var Q361;
            Q361=makeQuery(id+"F10.opPattern","COPY",BODY,{"derivedFrom":makeQuery(id+"F9.opPattern","COPY",BODY,{"derivedFrom":makeQuery(id+"F8.opPattern","COPY",BODY,{"derivedFrom":makeQuery(id+"F7.opPattern","COPY",BODY,{"derivedFrom":makeQuery(id+"F2.opPattern","COPY",BODY,{"derivedFrom":makeQuery(id+"F1.opRevolve","SWEPT_BODY",BODY,{"disambiguationData":[OSD([sQuery(id+"F0.wireOp",EDGE,"E1")])]}),"instanceName":"1"}),"instanceName":"1"}),"instanceName":"1"}),"instanceName":"1"}),"instanceName":"1"});
            var Q362;
            Q362=makeQuery(id+"F10.opPattern","COPY",BODY,{"derivedFrom":makeQuery(id+"F9.opPattern","COPY",BODY,{"derivedFrom":makeQuery(id+"F8.opPattern","COPY",BODY,{"derivedFrom":makeQuery(id+"F7.opPattern","COPY",BODY,{"derivedFrom":makeQuery(id+"F3.opPattern","COPY",BODY,{"derivedFrom":makeQuery(id+"F2.opPattern","COPY",BODY,{"derivedFrom":makeQuery(id+"F1.opRevolve","SWEPT_BODY",BODY,{"disambiguationData":[OSD([sQuery(id+"F0.wireOp",EDGE,"E1")])]}),"instanceName":"1"}),"instanceName":"1"}),"instanceName":"1"}),"instanceName":"1"}),"instanceName":"1"}),"instanceName":"1"});
            var Q363;
            Q363=makeQuery(id+"F10.opPattern","COPY",BODY,{"derivedFrom":makeQuery(id+"F9.opPattern","COPY",BODY,{"derivedFrom":makeQuery(id+"F8.opPattern","COPY",BODY,{"derivedFrom":makeQuery(id+"F7.opPattern","COPY",BODY,{"derivedFrom":makeQuery(id+"F4.opPattern","COPY",BODY,{"derivedFrom":makeQuery(id+"F1.opRevolve","SWEPT_BODY",BODY,{"disambiguationData":[OSD([sQuery(id+"F0.wireOp",EDGE,"E1")])]}),"instanceName":"1"}),"instanceName":"1"}),"instanceName":"1"}),"instanceName":"1"}),"instanceName":"1"});
            var Q364;
            Q364=makeQuery(id+"F10.opPattern","COPY",BODY,{"derivedFrom":makeQuery(id+"F9.opPattern","COPY",BODY,{"derivedFrom":makeQuery(id+"F8.opPattern","COPY",BODY,{"derivedFrom":makeQuery(id+"F7.opPattern","COPY",BODY,{"derivedFrom":makeQuery(id+"F4.opPattern","COPY",BODY,{"derivedFrom":makeQuery(id+"F2.opPattern","COPY",BODY,{"derivedFrom":makeQuery(id+"F1.opRevolve","SWEPT_BODY",BODY,{"disambiguationData":[OSD([sQuery(id+"F0.wireOp",EDGE,"E1")])]}),"instanceName":"1"}),"instanceName":"1"}),"instanceName":"1"}),"instanceName":"1"}),"instanceName":"1"}),"instanceName":"1"});
            var Q365;
            Q365=makeQuery(id+"F10.opPattern","COPY",BODY,{"derivedFrom":makeQuery(id+"F9.opPattern","COPY",BODY,{"derivedFrom":makeQuery(id+"F8.opPattern","COPY",BODY,{"derivedFrom":makeQuery(id+"F7.opPattern","COPY",BODY,{"derivedFrom":makeQuery(id+"F4.opPattern","COPY",BODY,{"derivedFrom":makeQuery(id+"F3.opPattern","COPY",BODY,{"derivedFrom":makeQuery(id+"F2.opPattern","COPY",BODY,{"derivedFrom":makeQuery(id+"F1.opRevolve","SWEPT_BODY",BODY,{"disambiguationData":[OSD([sQuery(id+"F0.wireOp",EDGE,"E1")])]}),"instanceName":"1"}),"instanceName":"1"}),"instanceName":"1"}),"instanceName":"1"}),"instanceName":"1"}),"instanceName":"1"}),"instanceName":"1"});
            var Q366;
            Q366=makeQuery(id+"F10.opPattern","COPY",BODY,{"derivedFrom":makeQuery(id+"F9.opPattern","COPY",BODY,{"derivedFrom":makeQuery(id+"F8.opPattern","COPY",BODY,{"derivedFrom":makeQuery(id+"F7.opPattern","COPY",BODY,{"derivedFrom":makeQuery(id+"F5.opPattern","COPY",BODY,{"derivedFrom":makeQuery(id+"F1.opRevolve","SWEPT_BODY",BODY,{"disambiguationData":[OSD([sQuery(id+"F0.wireOp",EDGE,"E1")])]}),"instanceName":"1"}),"instanceName":"1"}),"instanceName":"1"}),"instanceName":"1"}),"instanceName":"1"});
            var Q367;
            Q367=makeQuery(id+"F10.opPattern","COPY",BODY,{"derivedFrom":makeQuery(id+"F9.opPattern","COPY",BODY,{"derivedFrom":makeQuery(id+"F8.opPattern","COPY",BODY,{"derivedFrom":makeQuery(id+"F7.opPattern","COPY",BODY,{"derivedFrom":makeQuery(id+"F5.opPattern","COPY",BODY,{"derivedFrom":makeQuery(id+"F2.opPattern","COPY",BODY,{"derivedFrom":makeQuery(id+"F1.opRevolve","SWEPT_BODY",BODY,{"disambiguationData":[OSD([sQuery(id+"F0.wireOp",EDGE,"E1")])]}),"instanceName":"1"}),"instanceName":"1"}),"instanceName":"1"}),"instanceName":"1"}),"instanceName":"1"}),"instanceName":"1"});
            var Q368;
            Q368=makeQuery(id+"F10.opPattern","COPY",BODY,{"derivedFrom":makeQuery(id+"F9.opPattern","COPY",BODY,{"derivedFrom":makeQuery(id+"F8.opPattern","COPY",BODY,{"derivedFrom":makeQuery(id+"F7.opPattern","COPY",BODY,{"derivedFrom":makeQuery(id+"F5.opPattern","COPY",BODY,{"derivedFrom":makeQuery(id+"F3.opPattern","COPY",BODY,{"derivedFrom":makeQuery(id+"F2.opPattern","COPY",BODY,{"derivedFrom":makeQuery(id+"F1.opRevolve","SWEPT_BODY",BODY,{"disambiguationData":[OSD([sQuery(id+"F0.wireOp",EDGE,"E1")])]}),"instanceName":"1"}),"instanceName":"1"}),"instanceName":"1"}),"instanceName":"1"}),"instanceName":"1"}),"instanceName":"1"}),"instanceName":"1"});
            var Q369;
            Q369=makeQuery(id+"F10.opPattern","COPY",BODY,{"derivedFrom":makeQuery(id+"F9.opPattern","COPY",BODY,{"derivedFrom":makeQuery(id+"F8.opPattern","COPY",BODY,{"derivedFrom":makeQuery(id+"F7.opPattern","COPY",BODY,{"derivedFrom":makeQuery(id+"F5.opPattern","COPY",BODY,{"derivedFrom":makeQuery(id+"F4.opPattern","COPY",BODY,{"derivedFrom":makeQuery(id+"F1.opRevolve","SWEPT_BODY",BODY,{"disambiguationData":[OSD([sQuery(id+"F0.wireOp",EDGE,"E1")])]}),"instanceName":"1"}),"instanceName":"1"}),"instanceName":"1"}),"instanceName":"1"}),"instanceName":"1"}),"instanceName":"1"});
            var Q370;
            Q370=makeQuery(id+"F10.opPattern","COPY",BODY,{"derivedFrom":makeQuery(id+"F9.opPattern","COPY",BODY,{"derivedFrom":makeQuery(id+"F8.opPattern","COPY",BODY,{"derivedFrom":makeQuery(id+"F7.opPattern","COPY",BODY,{"derivedFrom":makeQuery(id+"F5.opPattern","COPY",BODY,{"derivedFrom":makeQuery(id+"F4.opPattern","COPY",BODY,{"derivedFrom":makeQuery(id+"F2.opPattern","COPY",BODY,{"derivedFrom":makeQuery(id+"F1.opRevolve","SWEPT_BODY",BODY,{"disambiguationData":[OSD([sQuery(id+"F0.wireOp",EDGE,"E1")])]}),"instanceName":"1"}),"instanceName":"1"}),"instanceName":"1"}),"instanceName":"1"}),"instanceName":"1"}),"instanceName":"1"}),"instanceName":"1"});
            var Q371;
            Q371=makeQuery(id+"F10.opPattern","COPY",BODY,{"derivedFrom":makeQuery(id+"F9.opPattern","COPY",BODY,{"derivedFrom":makeQuery(id+"F8.opPattern","COPY",BODY,{"derivedFrom":makeQuery(id+"F7.opPattern","COPY",BODY,{"derivedFrom":makeQuery(id+"F5.opPattern","COPY",BODY,{"derivedFrom":makeQuery(id+"F4.opPattern","COPY",BODY,{"derivedFrom":makeQuery(id+"F3.opPattern","COPY",BODY,{"derivedFrom":makeQuery(id+"F2.opPattern","COPY",BODY,{"derivedFrom":makeQuery(id+"F1.opRevolve","SWEPT_BODY",BODY,{"disambiguationData":[OSD([sQuery(id+"F0.wireOp",EDGE,"E1")])]}),"instanceName":"1"}),"instanceName":"1"}),"instanceName":"1"}),"instanceName":"1"}),"instanceName":"1"}),"instanceName":"1"}),"instanceName":"1"}),"instanceName":"1"});
            var Q372;
            Q372=makeQuery(id+"F10.opPattern","COPY",BODY,{"derivedFrom":makeQuery(id+"F9.opPattern","COPY",BODY,{"derivedFrom":makeQuery(id+"F8.opPattern","COPY",BODY,{"derivedFrom":makeQuery(id+"F7.opPattern","COPY",BODY,{"derivedFrom":makeQuery(id+"F6.opPattern","COPY",BODY,{"derivedFrom":makeQuery(id+"F1.opRevolve","SWEPT_BODY",BODY,{"disambiguationData":[OSD([sQuery(id+"F0.wireOp",EDGE,"E1")])]}),"instanceName":"1"}),"instanceName":"1"}),"instanceName":"1"}),"instanceName":"1"}),"instanceName":"1"});
            var Q373;
            Q373=makeQuery(id+"F10.opPattern","COPY",BODY,{"derivedFrom":makeQuery(id+"F9.opPattern","COPY",BODY,{"derivedFrom":makeQuery(id+"F8.opPattern","COPY",BODY,{"derivedFrom":makeQuery(id+"F7.opPattern","COPY",BODY,{"derivedFrom":makeQuery(id+"F6.opPattern","COPY",BODY,{"derivedFrom":makeQuery(id+"F2.opPattern","COPY",BODY,{"derivedFrom":makeQuery(id+"F1.opRevolve","SWEPT_BODY",BODY,{"disambiguationData":[OSD([sQuery(id+"F0.wireOp",EDGE,"E1")])]}),"instanceName":"1"}),"instanceName":"1"}),"instanceName":"1"}),"instanceName":"1"}),"instanceName":"1"}),"instanceName":"1"});
            var Q374;
            Q374=makeQuery(id+"F10.opPattern","COPY",BODY,{"derivedFrom":makeQuery(id+"F9.opPattern","COPY",BODY,{"derivedFrom":makeQuery(id+"F8.opPattern","COPY",BODY,{"derivedFrom":makeQuery(id+"F7.opPattern","COPY",BODY,{"derivedFrom":makeQuery(id+"F6.opPattern","COPY",BODY,{"derivedFrom":makeQuery(id+"F3.opPattern","COPY",BODY,{"derivedFrom":makeQuery(id+"F2.opPattern","COPY",BODY,{"derivedFrom":makeQuery(id+"F1.opRevolve","SWEPT_BODY",BODY,{"disambiguationData":[OSD([sQuery(id+"F0.wireOp",EDGE,"E1")])]}),"instanceName":"1"}),"instanceName":"1"}),"instanceName":"1"}),"instanceName":"1"}),"instanceName":"1"}),"instanceName":"1"}),"instanceName":"1"});
            var Q375;
            Q375=makeQuery(id+"F10.opPattern","COPY",BODY,{"derivedFrom":makeQuery(id+"F9.opPattern","COPY",BODY,{"derivedFrom":makeQuery(id+"F8.opPattern","COPY",BODY,{"derivedFrom":makeQuery(id+"F7.opPattern","COPY",BODY,{"derivedFrom":makeQuery(id+"F6.opPattern","COPY",BODY,{"derivedFrom":makeQuery(id+"F4.opPattern","COPY",BODY,{"derivedFrom":makeQuery(id+"F1.opRevolve","SWEPT_BODY",BODY,{"disambiguationData":[OSD([sQuery(id+"F0.wireOp",EDGE,"E1")])]}),"instanceName":"1"}),"instanceName":"1"}),"instanceName":"1"}),"instanceName":"1"}),"instanceName":"1"}),"instanceName":"1"});
            var Q376;
            Q376=makeQuery(id+"F10.opPattern","COPY",BODY,{"derivedFrom":makeQuery(id+"F9.opPattern","COPY",BODY,{"derivedFrom":makeQuery(id+"F8.opPattern","COPY",BODY,{"derivedFrom":makeQuery(id+"F7.opPattern","COPY",BODY,{"derivedFrom":makeQuery(id+"F6.opPattern","COPY",BODY,{"derivedFrom":makeQuery(id+"F4.opPattern","COPY",BODY,{"derivedFrom":makeQuery(id+"F2.opPattern","COPY",BODY,{"derivedFrom":makeQuery(id+"F1.opRevolve","SWEPT_BODY",BODY,{"disambiguationData":[OSD([sQuery(id+"F0.wireOp",EDGE,"E1")])]}),"instanceName":"1"}),"instanceName":"1"}),"instanceName":"1"}),"instanceName":"1"}),"instanceName":"1"}),"instanceName":"1"}),"instanceName":"1"});
            var Q377;
            Q377=makeQuery(id+"F10.opPattern","COPY",BODY,{"derivedFrom":makeQuery(id+"F9.opPattern","COPY",BODY,{"derivedFrom":makeQuery(id+"F8.opPattern","COPY",BODY,{"derivedFrom":makeQuery(id+"F7.opPattern","COPY",BODY,{"derivedFrom":makeQuery(id+"F6.opPattern","COPY",BODY,{"derivedFrom":makeQuery(id+"F4.opPattern","COPY",BODY,{"derivedFrom":makeQuery(id+"F3.opPattern","COPY",BODY,{"derivedFrom":makeQuery(id+"F2.opPattern","COPY",BODY,{"derivedFrom":makeQuery(id+"F1.opRevolve","SWEPT_BODY",BODY,{"disambiguationData":[OSD([sQuery(id+"F0.wireOp",EDGE,"E1")])]}),"instanceName":"1"}),"instanceName":"1"}),"instanceName":"1"}),"instanceName":"1"}),"instanceName":"1"}),"instanceName":"1"}),"instanceName":"1"}),"instanceName":"1"});
            var Q378;
            Q378=makeQuery(id+"F10.opPattern","COPY",BODY,{"derivedFrom":makeQuery(id+"F9.opPattern","COPY",BODY,{"derivedFrom":makeQuery(id+"F8.opPattern","COPY",BODY,{"derivedFrom":makeQuery(id+"F7.opPattern","COPY",BODY,{"derivedFrom":makeQuery(id+"F6.opPattern","COPY",BODY,{"derivedFrom":makeQuery(id+"F5.opPattern","COPY",BODY,{"derivedFrom":makeQuery(id+"F1.opRevolve","SWEPT_BODY",BODY,{"disambiguationData":[OSD([sQuery(id+"F0.wireOp",EDGE,"E1")])]}),"instanceName":"1"}),"instanceName":"1"}),"instanceName":"1"}),"instanceName":"1"}),"instanceName":"1"}),"instanceName":"1"});
            var Q379;
            Q379=makeQuery(id+"F10.opPattern","COPY",BODY,{"derivedFrom":makeQuery(id+"F9.opPattern","COPY",BODY,{"derivedFrom":makeQuery(id+"F8.opPattern","COPY",BODY,{"derivedFrom":makeQuery(id+"F7.opPattern","COPY",BODY,{"derivedFrom":makeQuery(id+"F6.opPattern","COPY",BODY,{"derivedFrom":makeQuery(id+"F5.opPattern","COPY",BODY,{"derivedFrom":makeQuery(id+"F2.opPattern","COPY",BODY,{"derivedFrom":makeQuery(id+"F1.opRevolve","SWEPT_BODY",BODY,{"disambiguationData":[OSD([sQuery(id+"F0.wireOp",EDGE,"E1")])]}),"instanceName":"1"}),"instanceName":"1"}),"instanceName":"1"}),"instanceName":"1"}),"instanceName":"1"}),"instanceName":"1"}),"instanceName":"1"});
            var Q380;
            Q380=makeQuery(id+"F10.opPattern","COPY",BODY,{"derivedFrom":makeQuery(id+"F9.opPattern","COPY",BODY,{"derivedFrom":makeQuery(id+"F8.opPattern","COPY",BODY,{"derivedFrom":makeQuery(id+"F7.opPattern","COPY",BODY,{"derivedFrom":makeQuery(id+"F6.opPattern","COPY",BODY,{"derivedFrom":makeQuery(id+"F5.opPattern","COPY",BODY,{"derivedFrom":makeQuery(id+"F3.opPattern","COPY",BODY,{"derivedFrom":makeQuery(id+"F2.opPattern","COPY",BODY,{"derivedFrom":makeQuery(id+"F1.opRevolve","SWEPT_BODY",BODY,{"disambiguationData":[OSD([sQuery(id+"F0.wireOp",EDGE,"E1")])]}),"instanceName":"1"}),"instanceName":"1"}),"instanceName":"1"}),"instanceName":"1"}),"instanceName":"1"}),"instanceName":"1"}),"instanceName":"1"}),"instanceName":"1"});
            var Q381;
            Q381=makeQuery(id+"F10.opPattern","COPY",BODY,{"derivedFrom":makeQuery(id+"F9.opPattern","COPY",BODY,{"derivedFrom":makeQuery(id+"F8.opPattern","COPY",BODY,{"derivedFrom":makeQuery(id+"F7.opPattern","COPY",BODY,{"derivedFrom":makeQuery(id+"F6.opPattern","COPY",BODY,{"derivedFrom":makeQuery(id+"F5.opPattern","COPY",BODY,{"derivedFrom":makeQuery(id+"F4.opPattern","COPY",BODY,{"derivedFrom":makeQuery(id+"F1.opRevolve","SWEPT_BODY",BODY,{"disambiguationData":[OSD([sQuery(id+"F0.wireOp",EDGE,"E1")])]}),"instanceName":"1"}),"instanceName":"1"}),"instanceName":"1"}),"instanceName":"1"}),"instanceName":"1"}),"instanceName":"1"}),"instanceName":"1"});
            var Q382;
            Q382=makeQuery(id+"F10.opPattern","COPY",BODY,{"derivedFrom":makeQuery(id+"F9.opPattern","COPY",BODY,{"derivedFrom":makeQuery(id+"F8.opPattern","COPY",BODY,{"derivedFrom":makeQuery(id+"F7.opPattern","COPY",BODY,{"derivedFrom":makeQuery(id+"F6.opPattern","COPY",BODY,{"derivedFrom":makeQuery(id+"F5.opPattern","COPY",BODY,{"derivedFrom":makeQuery(id+"F4.opPattern","COPY",BODY,{"derivedFrom":makeQuery(id+"F2.opPattern","COPY",BODY,{"derivedFrom":makeQuery(id+"F1.opRevolve","SWEPT_BODY",BODY,{"disambiguationData":[OSD([sQuery(id+"F0.wireOp",EDGE,"E1")])]}),"instanceName":"1"}),"instanceName":"1"}),"instanceName":"1"}),"instanceName":"1"}),"instanceName":"1"}),"instanceName":"1"}),"instanceName":"1"}),"instanceName":"1"});
            var Q383;
            Q383=makeQuery(id+"F10.opPattern","COPY",BODY,{"derivedFrom":makeQuery(id+"F9.opPattern","COPY",BODY,{"derivedFrom":makeQuery(id+"F8.opPattern","COPY",BODY,{"derivedFrom":makeQuery(id+"F7.opPattern","COPY",BODY,{"derivedFrom":makeQuery(id+"F6.opPattern","COPY",BODY,{"derivedFrom":makeQuery(id+"F5.opPattern","COPY",BODY,{"derivedFrom":makeQuery(id+"F4.opPattern","COPY",BODY,{"derivedFrom":makeQuery(id+"F3.opPattern","COPY",BODY,{"derivedFrom":makeQuery(id+"F2.opPattern","COPY",BODY,{"derivedFrom":makeQuery(id+"F1.opRevolve","SWEPT_BODY",BODY,{"disambiguationData":[OSD([sQuery(id+"F0.wireOp",EDGE,"E1")])]}),"instanceName":"1"}),"instanceName":"1"}),"instanceName":"1"}),"instanceName":"1"}),"instanceName":"1"}),"instanceName":"1"}),"instanceName":"1"}),"instanceName":"1"}),"instanceName":"1"});
            transform(context, id + "F11", {"entities" : qUnion([Q0, Q1, Q2, Q3, Q4, Q5, Q6, Q7, Q8, Q9, Q10, Q11, Q12, Q13, Q14, Q15, Q16, Q17, Q18, Q19, Q20, Q21, Q22, Q23, Q24, Q25, Q26, Q27, Q28, Q29, Q30, Q31, Q32, Q33, Q34, Q35, Q36, Q37, Q38, Q39, Q40, Q41, Q42, Q43, Q44, Q45, Q46, Q47, Q48, Q49, Q50, Q51, Q52, Q53, Q54, Q55, Q56, Q57, Q58, Q59, Q60, Q61, Q62, Q63, Q64, Q65, Q66, Q67, Q68, Q69, Q70, Q71, Q72, Q73, Q74, Q75, Q76, Q77, Q78, Q79, Q80, Q81, Q82, Q83, Q84, Q85, Q86, Q87, Q88, Q89, Q90, Q91, Q92, Q93, Q94, Q95, Q96, Q97, Q98, Q99, Q100, Q101, Q102, Q103, Q104, Q105, Q106, Q107, Q108, Q109, Q110, Q111, Q112, Q113, Q114, Q115, Q116, Q117, Q118, Q119, Q120, Q121, Q122, Q123, Q124, Q125, Q126, Q127, Q128, Q129, Q130, Q131, Q132, Q133, Q134, Q135, Q136, Q137, Q138, Q139, Q140, Q141, Q142, Q143, Q144, Q145, Q146, Q147, Q148, Q149, Q150, Q151, Q152, Q153, Q154, Q155, Q156, Q157, Q158, Q159, Q160, Q161, Q162, Q163, Q164, Q165, Q166, Q167, Q168, Q169, Q170, Q171, Q172, Q173, Q174, Q175, Q176, Q177, Q178, Q179, Q180, Q181, Q182, Q183, Q184, Q185, Q186, Q187, Q188, Q189, Q190, Q191, Q192, Q193, Q194, Q195, Q196, Q197, Q198, Q199, Q200, Q201, Q202, Q203, Q204, Q205, Q206, Q207, Q208, Q209, Q210, Q211, Q212, Q213, Q214, Q215, Q216, Q217, Q218, Q219, Q220, Q221, Q222, Q223, Q224, Q225, Q226, Q227, Q228, Q229, Q230, Q231, Q232, Q233, Q234, Q235, Q236, Q237, Q238, Q239, Q240, Q241, Q242, Q243, Q244, Q245, Q246, Q247, Q248, Q249, Q250, Q251, Q252, Q253, Q254, Q255, Q256, Q257, Q258, Q259, Q260, Q261, Q262, Q263, Q264, Q265, Q266, Q267, Q268, Q269, Q270, Q271, Q272, Q273, Q274, Q275, Q276, Q277, Q278, Q279, Q280, Q281, Q282, Q283, Q284, Q285, Q286, Q287, Q288, Q289, Q290, Q291, Q292, Q293, Q294, Q295, Q296, Q297, Q298, Q299, Q300, Q301, Q302, Q303, Q304, Q305, Q306, Q307, Q308, Q309, Q310, Q311, Q312, Q313, Q314, Q315, Q316, Q317, Q318, Q319, Q320, Q321, Q322, Q323, Q324, Q325, Q326, Q327, Q328, Q329, Q330, Q331, Q332, Q333, Q334, Q335, Q336, Q337, Q338, Q339, Q340, Q341, Q342, Q343, Q344, Q345, Q346, Q347, Q348, Q349, Q350, Q351, Q352, Q353, Q354, Q355, Q356, Q357, Q358, Q359, Q360, Q361, Q362, Q363, Q364, Q365, Q366, Q367, Q368, Q369, Q370, Q371, Q372, Q373, Q374, Q375, Q376, Q377, Q378, Q379, Q380, Q381, Q382, Q383]), "transformType" : TransformType.TRANSLATION_3D, "dx" : 0 * mm, "dy" : 0.28 * mm, "dz" : 0 * mm, "makeCopy" : true});
        }
        {
            var Q0;
            Q0=makeQuery(id+"F1.opRevolve","SWEPT_BODY",BODY,{"disambiguationData":[OSD([sQuery(id+"F0.wireOp",EDGE,"E1")])]});
            var Q1;
            Q1=makeQuery(id+"F2.opPattern","COPY",BODY,{"derivedFrom":makeQuery(id+"F1.opRevolve","SWEPT_BODY",BODY,{"disambiguationData":[OSD([sQuery(id+"F0.wireOp",EDGE,"E1")])]}),"instanceName":"1"});
            var Q2;
            Q2=makeQuery(id+"F3.opPattern","COPY",BODY,{"derivedFrom":makeQuery(id+"F2.opPattern","COPY",BODY,{"derivedFrom":makeQuery(id+"F1.opRevolve","SWEPT_BODY",BODY,{"disambiguationData":[OSD([sQuery(id+"F0.wireOp",EDGE,"E1")])]}),"instanceName":"1"}),"instanceName":"1"});
            var Q3;
            Q3=makeQuery(id+"F4.opPattern","COPY",BODY,{"derivedFrom":makeQuery(id+"F1.opRevolve","SWEPT_BODY",BODY,{"disambiguationData":[OSD([sQuery(id+"F0.wireOp",EDGE,"E1")])]}),"instanceName":"1"});
            var Q4;
            Q4=makeQuery(id+"F4.opPattern","COPY",BODY,{"derivedFrom":makeQuery(id+"F2.opPattern","COPY",BODY,{"derivedFrom":makeQuery(id+"F1.opRevolve","SWEPT_BODY",BODY,{"disambiguationData":[OSD([sQuery(id+"F0.wireOp",EDGE,"E1")])]}),"instanceName":"1"}),"instanceName":"1"});
            var Q5;
            Q5=makeQuery(id+"F4.opPattern","COPY",BODY,{"derivedFrom":makeQuery(id+"F3.opPattern","COPY",BODY,{"derivedFrom":makeQuery(id+"F2.opPattern","COPY",BODY,{"derivedFrom":makeQuery(id+"F1.opRevolve","SWEPT_BODY",BODY,{"disambiguationData":[OSD([sQuery(id+"F0.wireOp",EDGE,"E1")])]}),"instanceName":"1"}),"instanceName":"1"}),"instanceName":"1"});
            var Q6;
            Q6=makeQuery(id+"F5.opPattern","COPY",BODY,{"derivedFrom":makeQuery(id+"F1.opRevolve","SWEPT_BODY",BODY,{"disambiguationData":[OSD([sQuery(id+"F0.wireOp",EDGE,"E1")])]}),"instanceName":"1"});
            var Q7;
            Q7=makeQuery(id+"F5.opPattern","COPY",BODY,{"derivedFrom":makeQuery(id+"F2.opPattern","COPY",BODY,{"derivedFrom":makeQuery(id+"F1.opRevolve","SWEPT_BODY",BODY,{"disambiguationData":[OSD([sQuery(id+"F0.wireOp",EDGE,"E1")])]}),"instanceName":"1"}),"instanceName":"1"});
            var Q8;
            Q8=makeQuery(id+"F5.opPattern","COPY",BODY,{"derivedFrom":makeQuery(id+"F3.opPattern","COPY",BODY,{"derivedFrom":makeQuery(id+"F2.opPattern","COPY",BODY,{"derivedFrom":makeQuery(id+"F1.opRevolve","SWEPT_BODY",BODY,{"disambiguationData":[OSD([sQuery(id+"F0.wireOp",EDGE,"E1")])]}),"instanceName":"1"}),"instanceName":"1"}),"instanceName":"1"});
            var Q9;
            Q9=makeQuery(id+"F5.opPattern","COPY",BODY,{"derivedFrom":makeQuery(id+"F4.opPattern","COPY",BODY,{"derivedFrom":makeQuery(id+"F1.opRevolve","SWEPT_BODY",BODY,{"disambiguationData":[OSD([sQuery(id+"F0.wireOp",EDGE,"E1")])]}),"instanceName":"1"}),"instanceName":"1"});
            var Q10;
            Q10=makeQuery(id+"F5.opPattern","COPY",BODY,{"derivedFrom":makeQuery(id+"F4.opPattern","COPY",BODY,{"derivedFrom":makeQuery(id+"F2.opPattern","COPY",BODY,{"derivedFrom":makeQuery(id+"F1.opRevolve","SWEPT_BODY",BODY,{"disambiguationData":[OSD([sQuery(id+"F0.wireOp",EDGE,"E1")])]}),"instanceName":"1"}),"instanceName":"1"}),"instanceName":"1"});
            var Q11;
            Q11=makeQuery(id+"F5.opPattern","COPY",BODY,{"derivedFrom":makeQuery(id+"F4.opPattern","COPY",BODY,{"derivedFrom":makeQuery(id+"F3.opPattern","COPY",BODY,{"derivedFrom":makeQuery(id+"F2.opPattern","COPY",BODY,{"derivedFrom":makeQuery(id+"F1.opRevolve","SWEPT_BODY",BODY,{"disambiguationData":[OSD([sQuery(id+"F0.wireOp",EDGE,"E1")])]}),"instanceName":"1"}),"instanceName":"1"}),"instanceName":"1"}),"instanceName":"1"});
            var Q12;
            Q12=makeQuery(id+"F6.opPattern","COPY",BODY,{"derivedFrom":makeQuery(id+"F1.opRevolve","SWEPT_BODY",BODY,{"disambiguationData":[OSD([sQuery(id+"F0.wireOp",EDGE,"E1")])]}),"instanceName":"1"});
            var Q13;
            Q13=makeQuery(id+"F6.opPattern","COPY",BODY,{"derivedFrom":makeQuery(id+"F2.opPattern","COPY",BODY,{"derivedFrom":makeQuery(id+"F1.opRevolve","SWEPT_BODY",BODY,{"disambiguationData":[OSD([sQuery(id+"F0.wireOp",EDGE,"E1")])]}),"instanceName":"1"}),"instanceName":"1"});
            var Q14;
            Q14=makeQuery(id+"F6.opPattern","COPY",BODY,{"derivedFrom":makeQuery(id+"F3.opPattern","COPY",BODY,{"derivedFrom":makeQuery(id+"F2.opPattern","COPY",BODY,{"derivedFrom":makeQuery(id+"F1.opRevolve","SWEPT_BODY",BODY,{"disambiguationData":[OSD([sQuery(id+"F0.wireOp",EDGE,"E1")])]}),"instanceName":"1"}),"instanceName":"1"}),"instanceName":"1"});
            var Q15;
            Q15=makeQuery(id+"F6.opPattern","COPY",BODY,{"derivedFrom":makeQuery(id+"F4.opPattern","COPY",BODY,{"derivedFrom":makeQuery(id+"F1.opRevolve","SWEPT_BODY",BODY,{"disambiguationData":[OSD([sQuery(id+"F0.wireOp",EDGE,"E1")])]}),"instanceName":"1"}),"instanceName":"1"});
            var Q16;
            Q16=makeQuery(id+"F6.opPattern","COPY",BODY,{"derivedFrom":makeQuery(id+"F4.opPattern","COPY",BODY,{"derivedFrom":makeQuery(id+"F2.opPattern","COPY",BODY,{"derivedFrom":makeQuery(id+"F1.opRevolve","SWEPT_BODY",BODY,{"disambiguationData":[OSD([sQuery(id+"F0.wireOp",EDGE,"E1")])]}),"instanceName":"1"}),"instanceName":"1"}),"instanceName":"1"});
            var Q17;
            Q17=makeQuery(id+"F6.opPattern","COPY",BODY,{"derivedFrom":makeQuery(id+"F4.opPattern","COPY",BODY,{"derivedFrom":makeQuery(id+"F3.opPattern","COPY",BODY,{"derivedFrom":makeQuery(id+"F2.opPattern","COPY",BODY,{"derivedFrom":makeQuery(id+"F1.opRevolve","SWEPT_BODY",BODY,{"disambiguationData":[OSD([sQuery(id+"F0.wireOp",EDGE,"E1")])]}),"instanceName":"1"}),"instanceName":"1"}),"instanceName":"1"}),"instanceName":"1"});
            var Q18;
            Q18=makeQuery(id+"F6.opPattern","COPY",BODY,{"derivedFrom":makeQuery(id+"F5.opPattern","COPY",BODY,{"derivedFrom":makeQuery(id+"F1.opRevolve","SWEPT_BODY",BODY,{"disambiguationData":[OSD([sQuery(id+"F0.wireOp",EDGE,"E1")])]}),"instanceName":"1"}),"instanceName":"1"});
            var Q19;
            Q19=makeQuery(id+"F6.opPattern","COPY",BODY,{"derivedFrom":makeQuery(id+"F5.opPattern","COPY",BODY,{"derivedFrom":makeQuery(id+"F2.opPattern","COPY",BODY,{"derivedFrom":makeQuery(id+"F1.opRevolve","SWEPT_BODY",BODY,{"disambiguationData":[OSD([sQuery(id+"F0.wireOp",EDGE,"E1")])]}),"instanceName":"1"}),"instanceName":"1"}),"instanceName":"1"});
            var Q20;
            Q20=makeQuery(id+"F6.opPattern","COPY",BODY,{"derivedFrom":makeQuery(id+"F5.opPattern","COPY",BODY,{"derivedFrom":makeQuery(id+"F3.opPattern","COPY",BODY,{"derivedFrom":makeQuery(id+"F2.opPattern","COPY",BODY,{"derivedFrom":makeQuery(id+"F1.opRevolve","SWEPT_BODY",BODY,{"disambiguationData":[OSD([sQuery(id+"F0.wireOp",EDGE,"E1")])]}),"instanceName":"1"}),"instanceName":"1"}),"instanceName":"1"}),"instanceName":"1"});
            var Q21;
            Q21=makeQuery(id+"F6.opPattern","COPY",BODY,{"derivedFrom":makeQuery(id+"F5.opPattern","COPY",BODY,{"derivedFrom":makeQuery(id+"F4.opPattern","COPY",BODY,{"derivedFrom":makeQuery(id+"F1.opRevolve","SWEPT_BODY",BODY,{"disambiguationData":[OSD([sQuery(id+"F0.wireOp",EDGE,"E1")])]}),"instanceName":"1"}),"instanceName":"1"}),"instanceName":"1"});
            var Q22;
            Q22=makeQuery(id+"F6.opPattern","COPY",BODY,{"derivedFrom":makeQuery(id+"F5.opPattern","COPY",BODY,{"derivedFrom":makeQuery(id+"F4.opPattern","COPY",BODY,{"derivedFrom":makeQuery(id+"F2.opPattern","COPY",BODY,{"derivedFrom":makeQuery(id+"F1.opRevolve","SWEPT_BODY",BODY,{"disambiguationData":[OSD([sQuery(id+"F0.wireOp",EDGE,"E1")])]}),"instanceName":"1"}),"instanceName":"1"}),"instanceName":"1"}),"instanceName":"1"});
            var Q23;
            Q23=makeQuery(id+"F6.opPattern","COPY",BODY,{"derivedFrom":makeQuery(id+"F5.opPattern","COPY",BODY,{"derivedFrom":makeQuery(id+"F4.opPattern","COPY",BODY,{"derivedFrom":makeQuery(id+"F3.opPattern","COPY",BODY,{"derivedFrom":makeQuery(id+"F2.opPattern","COPY",BODY,{"derivedFrom":makeQuery(id+"F1.opRevolve","SWEPT_BODY",BODY,{"disambiguationData":[OSD([sQuery(id+"F0.wireOp",EDGE,"E1")])]}),"instanceName":"1"}),"instanceName":"1"}),"instanceName":"1"}),"instanceName":"1"}),"instanceName":"1"});
            var Q24;
            Q24=makeQuery(id+"F7.opPattern","COPY",BODY,{"derivedFrom":makeQuery(id+"F1.opRevolve","SWEPT_BODY",BODY,{"disambiguationData":[OSD([sQuery(id+"F0.wireOp",EDGE,"E1")])]}),"instanceName":"1"});
            var Q25;
            Q25=makeQuery(id+"F7.opPattern","COPY",BODY,{"derivedFrom":makeQuery(id+"F2.opPattern","COPY",BODY,{"derivedFrom":makeQuery(id+"F1.opRevolve","SWEPT_BODY",BODY,{"disambiguationData":[OSD([sQuery(id+"F0.wireOp",EDGE,"E1")])]}),"instanceName":"1"}),"instanceName":"1"});
            var Q26;
            Q26=makeQuery(id+"F7.opPattern","COPY",BODY,{"derivedFrom":makeQuery(id+"F3.opPattern","COPY",BODY,{"derivedFrom":makeQuery(id+"F2.opPattern","COPY",BODY,{"derivedFrom":makeQuery(id+"F1.opRevolve","SWEPT_BODY",BODY,{"disambiguationData":[OSD([sQuery(id+"F0.wireOp",EDGE,"E1")])]}),"instanceName":"1"}),"instanceName":"1"}),"instanceName":"1"});
            var Q27;
            Q27=makeQuery(id+"F7.opPattern","COPY",BODY,{"derivedFrom":makeQuery(id+"F4.opPattern","COPY",BODY,{"derivedFrom":makeQuery(id+"F1.opRevolve","SWEPT_BODY",BODY,{"disambiguationData":[OSD([sQuery(id+"F0.wireOp",EDGE,"E1")])]}),"instanceName":"1"}),"instanceName":"1"});
            var Q28;
            Q28=makeQuery(id+"F7.opPattern","COPY",BODY,{"derivedFrom":makeQuery(id+"F4.opPattern","COPY",BODY,{"derivedFrom":makeQuery(id+"F2.opPattern","COPY",BODY,{"derivedFrom":makeQuery(id+"F1.opRevolve","SWEPT_BODY",BODY,{"disambiguationData":[OSD([sQuery(id+"F0.wireOp",EDGE,"E1")])]}),"instanceName":"1"}),"instanceName":"1"}),"instanceName":"1"});
            var Q29;
            Q29=makeQuery(id+"F7.opPattern","COPY",BODY,{"derivedFrom":makeQuery(id+"F4.opPattern","COPY",BODY,{"derivedFrom":makeQuery(id+"F3.opPattern","COPY",BODY,{"derivedFrom":makeQuery(id+"F2.opPattern","COPY",BODY,{"derivedFrom":makeQuery(id+"F1.opRevolve","SWEPT_BODY",BODY,{"disambiguationData":[OSD([sQuery(id+"F0.wireOp",EDGE,"E1")])]}),"instanceName":"1"}),"instanceName":"1"}),"instanceName":"1"}),"instanceName":"1"});
            var Q30;
            Q30=makeQuery(id+"F7.opPattern","COPY",BODY,{"derivedFrom":makeQuery(id+"F5.opPattern","COPY",BODY,{"derivedFrom":makeQuery(id+"F1.opRevolve","SWEPT_BODY",BODY,{"disambiguationData":[OSD([sQuery(id+"F0.wireOp",EDGE,"E1")])]}),"instanceName":"1"}),"instanceName":"1"});
            var Q31;
            Q31=makeQuery(id+"F7.opPattern","COPY",BODY,{"derivedFrom":makeQuery(id+"F5.opPattern","COPY",BODY,{"derivedFrom":makeQuery(id+"F2.opPattern","COPY",BODY,{"derivedFrom":makeQuery(id+"F1.opRevolve","SWEPT_BODY",BODY,{"disambiguationData":[OSD([sQuery(id+"F0.wireOp",EDGE,"E1")])]}),"instanceName":"1"}),"instanceName":"1"}),"instanceName":"1"});
            var Q32;
            Q32=makeQuery(id+"F7.opPattern","COPY",BODY,{"derivedFrom":makeQuery(id+"F5.opPattern","COPY",BODY,{"derivedFrom":makeQuery(id+"F3.opPattern","COPY",BODY,{"derivedFrom":makeQuery(id+"F2.opPattern","COPY",BODY,{"derivedFrom":makeQuery(id+"F1.opRevolve","SWEPT_BODY",BODY,{"disambiguationData":[OSD([sQuery(id+"F0.wireOp",EDGE,"E1")])]}),"instanceName":"1"}),"instanceName":"1"}),"instanceName":"1"}),"instanceName":"1"});
            var Q33;
            Q33=makeQuery(id+"F7.opPattern","COPY",BODY,{"derivedFrom":makeQuery(id+"F5.opPattern","COPY",BODY,{"derivedFrom":makeQuery(id+"F4.opPattern","COPY",BODY,{"derivedFrom":makeQuery(id+"F1.opRevolve","SWEPT_BODY",BODY,{"disambiguationData":[OSD([sQuery(id+"F0.wireOp",EDGE,"E1")])]}),"instanceName":"1"}),"instanceName":"1"}),"instanceName":"1"});
            var Q34;
            Q34=makeQuery(id+"F7.opPattern","COPY",BODY,{"derivedFrom":makeQuery(id+"F5.opPattern","COPY",BODY,{"derivedFrom":makeQuery(id+"F4.opPattern","COPY",BODY,{"derivedFrom":makeQuery(id+"F2.opPattern","COPY",BODY,{"derivedFrom":makeQuery(id+"F1.opRevolve","SWEPT_BODY",BODY,{"disambiguationData":[OSD([sQuery(id+"F0.wireOp",EDGE,"E1")])]}),"instanceName":"1"}),"instanceName":"1"}),"instanceName":"1"}),"instanceName":"1"});
            var Q35;
            Q35=makeQuery(id+"F7.opPattern","COPY",BODY,{"derivedFrom":makeQuery(id+"F5.opPattern","COPY",BODY,{"derivedFrom":makeQuery(id+"F4.opPattern","COPY",BODY,{"derivedFrom":makeQuery(id+"F3.opPattern","COPY",BODY,{"derivedFrom":makeQuery(id+"F2.opPattern","COPY",BODY,{"derivedFrom":makeQuery(id+"F1.opRevolve","SWEPT_BODY",BODY,{"disambiguationData":[OSD([sQuery(id+"F0.wireOp",EDGE,"E1")])]}),"instanceName":"1"}),"instanceName":"1"}),"instanceName":"1"}),"instanceName":"1"}),"instanceName":"1"});
            var Q36;
            Q36=makeQuery(id+"F7.opPattern","COPY",BODY,{"derivedFrom":makeQuery(id+"F6.opPattern","COPY",BODY,{"derivedFrom":makeQuery(id+"F1.opRevolve","SWEPT_BODY",BODY,{"disambiguationData":[OSD([sQuery(id+"F0.wireOp",EDGE,"E1")])]}),"instanceName":"1"}),"instanceName":"1"});
            var Q37;
            Q37=makeQuery(id+"F7.opPattern","COPY",BODY,{"derivedFrom":makeQuery(id+"F6.opPattern","COPY",BODY,{"derivedFrom":makeQuery(id+"F2.opPattern","COPY",BODY,{"derivedFrom":makeQuery(id+"F1.opRevolve","SWEPT_BODY",BODY,{"disambiguationData":[OSD([sQuery(id+"F0.wireOp",EDGE,"E1")])]}),"instanceName":"1"}),"instanceName":"1"}),"instanceName":"1"});
            var Q38;
            Q38=makeQuery(id+"F7.opPattern","COPY",BODY,{"derivedFrom":makeQuery(id+"F6.opPattern","COPY",BODY,{"derivedFrom":makeQuery(id+"F3.opPattern","COPY",BODY,{"derivedFrom":makeQuery(id+"F2.opPattern","COPY",BODY,{"derivedFrom":makeQuery(id+"F1.opRevolve","SWEPT_BODY",BODY,{"disambiguationData":[OSD([sQuery(id+"F0.wireOp",EDGE,"E1")])]}),"instanceName":"1"}),"instanceName":"1"}),"instanceName":"1"}),"instanceName":"1"});
            var Q39;
            Q39=makeQuery(id+"F7.opPattern","COPY",BODY,{"derivedFrom":makeQuery(id+"F6.opPattern","COPY",BODY,{"derivedFrom":makeQuery(id+"F4.opPattern","COPY",BODY,{"derivedFrom":makeQuery(id+"F1.opRevolve","SWEPT_BODY",BODY,{"disambiguationData":[OSD([sQuery(id+"F0.wireOp",EDGE,"E1")])]}),"instanceName":"1"}),"instanceName":"1"}),"instanceName":"1"});
            var Q40;
            Q40=makeQuery(id+"F7.opPattern","COPY",BODY,{"derivedFrom":makeQuery(id+"F6.opPattern","COPY",BODY,{"derivedFrom":makeQuery(id+"F4.opPattern","COPY",BODY,{"derivedFrom":makeQuery(id+"F2.opPattern","COPY",BODY,{"derivedFrom":makeQuery(id+"F1.opRevolve","SWEPT_BODY",BODY,{"disambiguationData":[OSD([sQuery(id+"F0.wireOp",EDGE,"E1")])]}),"instanceName":"1"}),"instanceName":"1"}),"instanceName":"1"}),"instanceName":"1"});
            var Q41;
            Q41=makeQuery(id+"F7.opPattern","COPY",BODY,{"derivedFrom":makeQuery(id+"F6.opPattern","COPY",BODY,{"derivedFrom":makeQuery(id+"F4.opPattern","COPY",BODY,{"derivedFrom":makeQuery(id+"F3.opPattern","COPY",BODY,{"derivedFrom":makeQuery(id+"F2.opPattern","COPY",BODY,{"derivedFrom":makeQuery(id+"F1.opRevolve","SWEPT_BODY",BODY,{"disambiguationData":[OSD([sQuery(id+"F0.wireOp",EDGE,"E1")])]}),"instanceName":"1"}),"instanceName":"1"}),"instanceName":"1"}),"instanceName":"1"}),"instanceName":"1"});
            var Q42;
            Q42=makeQuery(id+"F7.opPattern","COPY",BODY,{"derivedFrom":makeQuery(id+"F6.opPattern","COPY",BODY,{"derivedFrom":makeQuery(id+"F5.opPattern","COPY",BODY,{"derivedFrom":makeQuery(id+"F1.opRevolve","SWEPT_BODY",BODY,{"disambiguationData":[OSD([sQuery(id+"F0.wireOp",EDGE,"E1")])]}),"instanceName":"1"}),"instanceName":"1"}),"instanceName":"1"});
            var Q43;
            Q43=makeQuery(id+"F7.opPattern","COPY",BODY,{"derivedFrom":makeQuery(id+"F6.opPattern","COPY",BODY,{"derivedFrom":makeQuery(id+"F5.opPattern","COPY",BODY,{"derivedFrom":makeQuery(id+"F2.opPattern","COPY",BODY,{"derivedFrom":makeQuery(id+"F1.opRevolve","SWEPT_BODY",BODY,{"disambiguationData":[OSD([sQuery(id+"F0.wireOp",EDGE,"E1")])]}),"instanceName":"1"}),"instanceName":"1"}),"instanceName":"1"}),"instanceName":"1"});
            var Q44;
            Q44=makeQuery(id+"F7.opPattern","COPY",BODY,{"derivedFrom":makeQuery(id+"F6.opPattern","COPY",BODY,{"derivedFrom":makeQuery(id+"F5.opPattern","COPY",BODY,{"derivedFrom":makeQuery(id+"F3.opPattern","COPY",BODY,{"derivedFrom":makeQuery(id+"F2.opPattern","COPY",BODY,{"derivedFrom":makeQuery(id+"F1.opRevolve","SWEPT_BODY",BODY,{"disambiguationData":[OSD([sQuery(id+"F0.wireOp",EDGE,"E1")])]}),"instanceName":"1"}),"instanceName":"1"}),"instanceName":"1"}),"instanceName":"1"}),"instanceName":"1"});
            var Q45;
            Q45=makeQuery(id+"F7.opPattern","COPY",BODY,{"derivedFrom":makeQuery(id+"F6.opPattern","COPY",BODY,{"derivedFrom":makeQuery(id+"F5.opPattern","COPY",BODY,{"derivedFrom":makeQuery(id+"F4.opPattern","COPY",BODY,{"derivedFrom":makeQuery(id+"F1.opRevolve","SWEPT_BODY",BODY,{"disambiguationData":[OSD([sQuery(id+"F0.wireOp",EDGE,"E1")])]}),"instanceName":"1"}),"instanceName":"1"}),"instanceName":"1"}),"instanceName":"1"});
            var Q46;
            Q46=makeQuery(id+"F7.opPattern","COPY",BODY,{"derivedFrom":makeQuery(id+"F6.opPattern","COPY",BODY,{"derivedFrom":makeQuery(id+"F5.opPattern","COPY",BODY,{"derivedFrom":makeQuery(id+"F4.opPattern","COPY",BODY,{"derivedFrom":makeQuery(id+"F2.opPattern","COPY",BODY,{"derivedFrom":makeQuery(id+"F1.opRevolve","SWEPT_BODY",BODY,{"disambiguationData":[OSD([sQuery(id+"F0.wireOp",EDGE,"E1")])]}),"instanceName":"1"}),"instanceName":"1"}),"instanceName":"1"}),"instanceName":"1"}),"instanceName":"1"});
            var Q47;
            Q47=makeQuery(id+"F7.opPattern","COPY",BODY,{"derivedFrom":makeQuery(id+"F6.opPattern","COPY",BODY,{"derivedFrom":makeQuery(id+"F5.opPattern","COPY",BODY,{"derivedFrom":makeQuery(id+"F4.opPattern","COPY",BODY,{"derivedFrom":makeQuery(id+"F3.opPattern","COPY",BODY,{"derivedFrom":makeQuery(id+"F2.opPattern","COPY",BODY,{"derivedFrom":makeQuery(id+"F1.opRevolve","SWEPT_BODY",BODY,{"disambiguationData":[OSD([sQuery(id+"F0.wireOp",EDGE,"E1")])]}),"instanceName":"1"}),"instanceName":"1"}),"instanceName":"1"}),"instanceName":"1"}),"instanceName":"1"}),"instanceName":"1"});
            var Q48;
            Q48=makeQuery(id+"F8.opPattern","COPY",BODY,{"derivedFrom":makeQuery(id+"F1.opRevolve","SWEPT_BODY",BODY,{"disambiguationData":[OSD([sQuery(id+"F0.wireOp",EDGE,"E1")])]}),"instanceName":"1"});
            var Q49;
            Q49=makeQuery(id+"F8.opPattern","COPY",BODY,{"derivedFrom":makeQuery(id+"F2.opPattern","COPY",BODY,{"derivedFrom":makeQuery(id+"F1.opRevolve","SWEPT_BODY",BODY,{"disambiguationData":[OSD([sQuery(id+"F0.wireOp",EDGE,"E1")])]}),"instanceName":"1"}),"instanceName":"1"});
            var Q50;
            Q50=makeQuery(id+"F8.opPattern","COPY",BODY,{"derivedFrom":makeQuery(id+"F3.opPattern","COPY",BODY,{"derivedFrom":makeQuery(id+"F2.opPattern","COPY",BODY,{"derivedFrom":makeQuery(id+"F1.opRevolve","SWEPT_BODY",BODY,{"disambiguationData":[OSD([sQuery(id+"F0.wireOp",EDGE,"E1")])]}),"instanceName":"1"}),"instanceName":"1"}),"instanceName":"1"});
            var Q51;
            Q51=makeQuery(id+"F8.opPattern","COPY",BODY,{"derivedFrom":makeQuery(id+"F4.opPattern","COPY",BODY,{"derivedFrom":makeQuery(id+"F1.opRevolve","SWEPT_BODY",BODY,{"disambiguationData":[OSD([sQuery(id+"F0.wireOp",EDGE,"E1")])]}),"instanceName":"1"}),"instanceName":"1"});
            var Q52;
            Q52=makeQuery(id+"F8.opPattern","COPY",BODY,{"derivedFrom":makeQuery(id+"F4.opPattern","COPY",BODY,{"derivedFrom":makeQuery(id+"F2.opPattern","COPY",BODY,{"derivedFrom":makeQuery(id+"F1.opRevolve","SWEPT_BODY",BODY,{"disambiguationData":[OSD([sQuery(id+"F0.wireOp",EDGE,"E1")])]}),"instanceName":"1"}),"instanceName":"1"}),"instanceName":"1"});
            var Q53;
            Q53=makeQuery(id+"F8.opPattern","COPY",BODY,{"derivedFrom":makeQuery(id+"F4.opPattern","COPY",BODY,{"derivedFrom":makeQuery(id+"F3.opPattern","COPY",BODY,{"derivedFrom":makeQuery(id+"F2.opPattern","COPY",BODY,{"derivedFrom":makeQuery(id+"F1.opRevolve","SWEPT_BODY",BODY,{"disambiguationData":[OSD([sQuery(id+"F0.wireOp",EDGE,"E1")])]}),"instanceName":"1"}),"instanceName":"1"}),"instanceName":"1"}),"instanceName":"1"});
            var Q54;
            Q54=makeQuery(id+"F8.opPattern","COPY",BODY,{"derivedFrom":makeQuery(id+"F5.opPattern","COPY",BODY,{"derivedFrom":makeQuery(id+"F1.opRevolve","SWEPT_BODY",BODY,{"disambiguationData":[OSD([sQuery(id+"F0.wireOp",EDGE,"E1")])]}),"instanceName":"1"}),"instanceName":"1"});
            var Q55;
            Q55=makeQuery(id+"F8.opPattern","COPY",BODY,{"derivedFrom":makeQuery(id+"F5.opPattern","COPY",BODY,{"derivedFrom":makeQuery(id+"F2.opPattern","COPY",BODY,{"derivedFrom":makeQuery(id+"F1.opRevolve","SWEPT_BODY",BODY,{"disambiguationData":[OSD([sQuery(id+"F0.wireOp",EDGE,"E1")])]}),"instanceName":"1"}),"instanceName":"1"}),"instanceName":"1"});
            var Q56;
            Q56=makeQuery(id+"F8.opPattern","COPY",BODY,{"derivedFrom":makeQuery(id+"F5.opPattern","COPY",BODY,{"derivedFrom":makeQuery(id+"F3.opPattern","COPY",BODY,{"derivedFrom":makeQuery(id+"F2.opPattern","COPY",BODY,{"derivedFrom":makeQuery(id+"F1.opRevolve","SWEPT_BODY",BODY,{"disambiguationData":[OSD([sQuery(id+"F0.wireOp",EDGE,"E1")])]}),"instanceName":"1"}),"instanceName":"1"}),"instanceName":"1"}),"instanceName":"1"});
            var Q57;
            Q57=makeQuery(id+"F8.opPattern","COPY",BODY,{"derivedFrom":makeQuery(id+"F5.opPattern","COPY",BODY,{"derivedFrom":makeQuery(id+"F4.opPattern","COPY",BODY,{"derivedFrom":makeQuery(id+"F1.opRevolve","SWEPT_BODY",BODY,{"disambiguationData":[OSD([sQuery(id+"F0.wireOp",EDGE,"E1")])]}),"instanceName":"1"}),"instanceName":"1"}),"instanceName":"1"});
            var Q58;
            Q58=makeQuery(id+"F8.opPattern","COPY",BODY,{"derivedFrom":makeQuery(id+"F5.opPattern","COPY",BODY,{"derivedFrom":makeQuery(id+"F4.opPattern","COPY",BODY,{"derivedFrom":makeQuery(id+"F2.opPattern","COPY",BODY,{"derivedFrom":makeQuery(id+"F1.opRevolve","SWEPT_BODY",BODY,{"disambiguationData":[OSD([sQuery(id+"F0.wireOp",EDGE,"E1")])]}),"instanceName":"1"}),"instanceName":"1"}),"instanceName":"1"}),"instanceName":"1"});
            var Q59;
            Q59=makeQuery(id+"F8.opPattern","COPY",BODY,{"derivedFrom":makeQuery(id+"F5.opPattern","COPY",BODY,{"derivedFrom":makeQuery(id+"F4.opPattern","COPY",BODY,{"derivedFrom":makeQuery(id+"F3.opPattern","COPY",BODY,{"derivedFrom":makeQuery(id+"F2.opPattern","COPY",BODY,{"derivedFrom":makeQuery(id+"F1.opRevolve","SWEPT_BODY",BODY,{"disambiguationData":[OSD([sQuery(id+"F0.wireOp",EDGE,"E1")])]}),"instanceName":"1"}),"instanceName":"1"}),"instanceName":"1"}),"instanceName":"1"}),"instanceName":"1"});
            var Q60;
            Q60=makeQuery(id+"F8.opPattern","COPY",BODY,{"derivedFrom":makeQuery(id+"F6.opPattern","COPY",BODY,{"derivedFrom":makeQuery(id+"F1.opRevolve","SWEPT_BODY",BODY,{"disambiguationData":[OSD([sQuery(id+"F0.wireOp",EDGE,"E1")])]}),"instanceName":"1"}),"instanceName":"1"});
            var Q61;
            Q61=makeQuery(id+"F8.opPattern","COPY",BODY,{"derivedFrom":makeQuery(id+"F6.opPattern","COPY",BODY,{"derivedFrom":makeQuery(id+"F2.opPattern","COPY",BODY,{"derivedFrom":makeQuery(id+"F1.opRevolve","SWEPT_BODY",BODY,{"disambiguationData":[OSD([sQuery(id+"F0.wireOp",EDGE,"E1")])]}),"instanceName":"1"}),"instanceName":"1"}),"instanceName":"1"});
            var Q62;
            Q62=makeQuery(id+"F8.opPattern","COPY",BODY,{"derivedFrom":makeQuery(id+"F6.opPattern","COPY",BODY,{"derivedFrom":makeQuery(id+"F3.opPattern","COPY",BODY,{"derivedFrom":makeQuery(id+"F2.opPattern","COPY",BODY,{"derivedFrom":makeQuery(id+"F1.opRevolve","SWEPT_BODY",BODY,{"disambiguationData":[OSD([sQuery(id+"F0.wireOp",EDGE,"E1")])]}),"instanceName":"1"}),"instanceName":"1"}),"instanceName":"1"}),"instanceName":"1"});
            var Q63;
            Q63=makeQuery(id+"F8.opPattern","COPY",BODY,{"derivedFrom":makeQuery(id+"F6.opPattern","COPY",BODY,{"derivedFrom":makeQuery(id+"F4.opPattern","COPY",BODY,{"derivedFrom":makeQuery(id+"F1.opRevolve","SWEPT_BODY",BODY,{"disambiguationData":[OSD([sQuery(id+"F0.wireOp",EDGE,"E1")])]}),"instanceName":"1"}),"instanceName":"1"}),"instanceName":"1"});
            var Q64;
            Q64=makeQuery(id+"F8.opPattern","COPY",BODY,{"derivedFrom":makeQuery(id+"F6.opPattern","COPY",BODY,{"derivedFrom":makeQuery(id+"F4.opPattern","COPY",BODY,{"derivedFrom":makeQuery(id+"F2.opPattern","COPY",BODY,{"derivedFrom":makeQuery(id+"F1.opRevolve","SWEPT_BODY",BODY,{"disambiguationData":[OSD([sQuery(id+"F0.wireOp",EDGE,"E1")])]}),"instanceName":"1"}),"instanceName":"1"}),"instanceName":"1"}),"instanceName":"1"});
            var Q65;
            Q65=makeQuery(id+"F8.opPattern","COPY",BODY,{"derivedFrom":makeQuery(id+"F6.opPattern","COPY",BODY,{"derivedFrom":makeQuery(id+"F4.opPattern","COPY",BODY,{"derivedFrom":makeQuery(id+"F3.opPattern","COPY",BODY,{"derivedFrom":makeQuery(id+"F2.opPattern","COPY",BODY,{"derivedFrom":makeQuery(id+"F1.opRevolve","SWEPT_BODY",BODY,{"disambiguationData":[OSD([sQuery(id+"F0.wireOp",EDGE,"E1")])]}),"instanceName":"1"}),"instanceName":"1"}),"instanceName":"1"}),"instanceName":"1"}),"instanceName":"1"});
            var Q66;
            Q66=makeQuery(id+"F8.opPattern","COPY",BODY,{"derivedFrom":makeQuery(id+"F6.opPattern","COPY",BODY,{"derivedFrom":makeQuery(id+"F5.opPattern","COPY",BODY,{"derivedFrom":makeQuery(id+"F1.opRevolve","SWEPT_BODY",BODY,{"disambiguationData":[OSD([sQuery(id+"F0.wireOp",EDGE,"E1")])]}),"instanceName":"1"}),"instanceName":"1"}),"instanceName":"1"});
            var Q67;
            Q67=makeQuery(id+"F8.opPattern","COPY",BODY,{"derivedFrom":makeQuery(id+"F6.opPattern","COPY",BODY,{"derivedFrom":makeQuery(id+"F5.opPattern","COPY",BODY,{"derivedFrom":makeQuery(id+"F2.opPattern","COPY",BODY,{"derivedFrom":makeQuery(id+"F1.opRevolve","SWEPT_BODY",BODY,{"disambiguationData":[OSD([sQuery(id+"F0.wireOp",EDGE,"E1")])]}),"instanceName":"1"}),"instanceName":"1"}),"instanceName":"1"}),"instanceName":"1"});
            var Q68;
            Q68=makeQuery(id+"F8.opPattern","COPY",BODY,{"derivedFrom":makeQuery(id+"F6.opPattern","COPY",BODY,{"derivedFrom":makeQuery(id+"F5.opPattern","COPY",BODY,{"derivedFrom":makeQuery(id+"F3.opPattern","COPY",BODY,{"derivedFrom":makeQuery(id+"F2.opPattern","COPY",BODY,{"derivedFrom":makeQuery(id+"F1.opRevolve","SWEPT_BODY",BODY,{"disambiguationData":[OSD([sQuery(id+"F0.wireOp",EDGE,"E1")])]}),"instanceName":"1"}),"instanceName":"1"}),"instanceName":"1"}),"instanceName":"1"}),"instanceName":"1"});
            var Q69;
            Q69=makeQuery(id+"F8.opPattern","COPY",BODY,{"derivedFrom":makeQuery(id+"F6.opPattern","COPY",BODY,{"derivedFrom":makeQuery(id+"F5.opPattern","COPY",BODY,{"derivedFrom":makeQuery(id+"F4.opPattern","COPY",BODY,{"derivedFrom":makeQuery(id+"F1.opRevolve","SWEPT_BODY",BODY,{"disambiguationData":[OSD([sQuery(id+"F0.wireOp",EDGE,"E1")])]}),"instanceName":"1"}),"instanceName":"1"}),"instanceName":"1"}),"instanceName":"1"});
            var Q70;
            Q70=makeQuery(id+"F8.opPattern","COPY",BODY,{"derivedFrom":makeQuery(id+"F6.opPattern","COPY",BODY,{"derivedFrom":makeQuery(id+"F5.opPattern","COPY",BODY,{"derivedFrom":makeQuery(id+"F4.opPattern","COPY",BODY,{"derivedFrom":makeQuery(id+"F2.opPattern","COPY",BODY,{"derivedFrom":makeQuery(id+"F1.opRevolve","SWEPT_BODY",BODY,{"disambiguationData":[OSD([sQuery(id+"F0.wireOp",EDGE,"E1")])]}),"instanceName":"1"}),"instanceName":"1"}),"instanceName":"1"}),"instanceName":"1"}),"instanceName":"1"});
            var Q71;
            Q71=makeQuery(id+"F8.opPattern","COPY",BODY,{"derivedFrom":makeQuery(id+"F6.opPattern","COPY",BODY,{"derivedFrom":makeQuery(id+"F5.opPattern","COPY",BODY,{"derivedFrom":makeQuery(id+"F4.opPattern","COPY",BODY,{"derivedFrom":makeQuery(id+"F3.opPattern","COPY",BODY,{"derivedFrom":makeQuery(id+"F2.opPattern","COPY",BODY,{"derivedFrom":makeQuery(id+"F1.opRevolve","SWEPT_BODY",BODY,{"disambiguationData":[OSD([sQuery(id+"F0.wireOp",EDGE,"E1")])]}),"instanceName":"1"}),"instanceName":"1"}),"instanceName":"1"}),"instanceName":"1"}),"instanceName":"1"}),"instanceName":"1"});
            var Q72;
            Q72=makeQuery(id+"F8.opPattern","COPY",BODY,{"derivedFrom":makeQuery(id+"F7.opPattern","COPY",BODY,{"derivedFrom":makeQuery(id+"F1.opRevolve","SWEPT_BODY",BODY,{"disambiguationData":[OSD([sQuery(id+"F0.wireOp",EDGE,"E1")])]}),"instanceName":"1"}),"instanceName":"1"});
            var Q73;
            Q73=makeQuery(id+"F8.opPattern","COPY",BODY,{"derivedFrom":makeQuery(id+"F7.opPattern","COPY",BODY,{"derivedFrom":makeQuery(id+"F2.opPattern","COPY",BODY,{"derivedFrom":makeQuery(id+"F1.opRevolve","SWEPT_BODY",BODY,{"disambiguationData":[OSD([sQuery(id+"F0.wireOp",EDGE,"E1")])]}),"instanceName":"1"}),"instanceName":"1"}),"instanceName":"1"});
            var Q74;
            Q74=makeQuery(id+"F8.opPattern","COPY",BODY,{"derivedFrom":makeQuery(id+"F7.opPattern","COPY",BODY,{"derivedFrom":makeQuery(id+"F3.opPattern","COPY",BODY,{"derivedFrom":makeQuery(id+"F2.opPattern","COPY",BODY,{"derivedFrom":makeQuery(id+"F1.opRevolve","SWEPT_BODY",BODY,{"disambiguationData":[OSD([sQuery(id+"F0.wireOp",EDGE,"E1")])]}),"instanceName":"1"}),"instanceName":"1"}),"instanceName":"1"}),"instanceName":"1"});
            var Q75;
            Q75=makeQuery(id+"F8.opPattern","COPY",BODY,{"derivedFrom":makeQuery(id+"F7.opPattern","COPY",BODY,{"derivedFrom":makeQuery(id+"F4.opPattern","COPY",BODY,{"derivedFrom":makeQuery(id+"F1.opRevolve","SWEPT_BODY",BODY,{"disambiguationData":[OSD([sQuery(id+"F0.wireOp",EDGE,"E1")])]}),"instanceName":"1"}),"instanceName":"1"}),"instanceName":"1"});
            var Q76;
            Q76=makeQuery(id+"F8.opPattern","COPY",BODY,{"derivedFrom":makeQuery(id+"F7.opPattern","COPY",BODY,{"derivedFrom":makeQuery(id+"F4.opPattern","COPY",BODY,{"derivedFrom":makeQuery(id+"F2.opPattern","COPY",BODY,{"derivedFrom":makeQuery(id+"F1.opRevolve","SWEPT_BODY",BODY,{"disambiguationData":[OSD([sQuery(id+"F0.wireOp",EDGE,"E1")])]}),"instanceName":"1"}),"instanceName":"1"}),"instanceName":"1"}),"instanceName":"1"});
            var Q77;
            Q77=makeQuery(id+"F8.opPattern","COPY",BODY,{"derivedFrom":makeQuery(id+"F7.opPattern","COPY",BODY,{"derivedFrom":makeQuery(id+"F4.opPattern","COPY",BODY,{"derivedFrom":makeQuery(id+"F3.opPattern","COPY",BODY,{"derivedFrom":makeQuery(id+"F2.opPattern","COPY",BODY,{"derivedFrom":makeQuery(id+"F1.opRevolve","SWEPT_BODY",BODY,{"disambiguationData":[OSD([sQuery(id+"F0.wireOp",EDGE,"E1")])]}),"instanceName":"1"}),"instanceName":"1"}),"instanceName":"1"}),"instanceName":"1"}),"instanceName":"1"});
            var Q78;
            Q78=makeQuery(id+"F8.opPattern","COPY",BODY,{"derivedFrom":makeQuery(id+"F7.opPattern","COPY",BODY,{"derivedFrom":makeQuery(id+"F5.opPattern","COPY",BODY,{"derivedFrom":makeQuery(id+"F1.opRevolve","SWEPT_BODY",BODY,{"disambiguationData":[OSD([sQuery(id+"F0.wireOp",EDGE,"E1")])]}),"instanceName":"1"}),"instanceName":"1"}),"instanceName":"1"});
            var Q79;
            Q79=makeQuery(id+"F8.opPattern","COPY",BODY,{"derivedFrom":makeQuery(id+"F7.opPattern","COPY",BODY,{"derivedFrom":makeQuery(id+"F5.opPattern","COPY",BODY,{"derivedFrom":makeQuery(id+"F2.opPattern","COPY",BODY,{"derivedFrom":makeQuery(id+"F1.opRevolve","SWEPT_BODY",BODY,{"disambiguationData":[OSD([sQuery(id+"F0.wireOp",EDGE,"E1")])]}),"instanceName":"1"}),"instanceName":"1"}),"instanceName":"1"}),"instanceName":"1"});
            var Q80;
            Q80=makeQuery(id+"F8.opPattern","COPY",BODY,{"derivedFrom":makeQuery(id+"F7.opPattern","COPY",BODY,{"derivedFrom":makeQuery(id+"F5.opPattern","COPY",BODY,{"derivedFrom":makeQuery(id+"F3.opPattern","COPY",BODY,{"derivedFrom":makeQuery(id+"F2.opPattern","COPY",BODY,{"derivedFrom":makeQuery(id+"F1.opRevolve","SWEPT_BODY",BODY,{"disambiguationData":[OSD([sQuery(id+"F0.wireOp",EDGE,"E1")])]}),"instanceName":"1"}),"instanceName":"1"}),"instanceName":"1"}),"instanceName":"1"}),"instanceName":"1"});
            var Q81;
            Q81=makeQuery(id+"F8.opPattern","COPY",BODY,{"derivedFrom":makeQuery(id+"F7.opPattern","COPY",BODY,{"derivedFrom":makeQuery(id+"F5.opPattern","COPY",BODY,{"derivedFrom":makeQuery(id+"F4.opPattern","COPY",BODY,{"derivedFrom":makeQuery(id+"F1.opRevolve","SWEPT_BODY",BODY,{"disambiguationData":[OSD([sQuery(id+"F0.wireOp",EDGE,"E1")])]}),"instanceName":"1"}),"instanceName":"1"}),"instanceName":"1"}),"instanceName":"1"});
            var Q82;
            Q82=makeQuery(id+"F8.opPattern","COPY",BODY,{"derivedFrom":makeQuery(id+"F7.opPattern","COPY",BODY,{"derivedFrom":makeQuery(id+"F5.opPattern","COPY",BODY,{"derivedFrom":makeQuery(id+"F4.opPattern","COPY",BODY,{"derivedFrom":makeQuery(id+"F2.opPattern","COPY",BODY,{"derivedFrom":makeQuery(id+"F1.opRevolve","SWEPT_BODY",BODY,{"disambiguationData":[OSD([sQuery(id+"F0.wireOp",EDGE,"E1")])]}),"instanceName":"1"}),"instanceName":"1"}),"instanceName":"1"}),"instanceName":"1"}),"instanceName":"1"});
            var Q83;
            Q83=makeQuery(id+"F8.opPattern","COPY",BODY,{"derivedFrom":makeQuery(id+"F7.opPattern","COPY",BODY,{"derivedFrom":makeQuery(id+"F5.opPattern","COPY",BODY,{"derivedFrom":makeQuery(id+"F4.opPattern","COPY",BODY,{"derivedFrom":makeQuery(id+"F3.opPattern","COPY",BODY,{"derivedFrom":makeQuery(id+"F2.opPattern","COPY",BODY,{"derivedFrom":makeQuery(id+"F1.opRevolve","SWEPT_BODY",BODY,{"disambiguationData":[OSD([sQuery(id+"F0.wireOp",EDGE,"E1")])]}),"instanceName":"1"}),"instanceName":"1"}),"instanceName":"1"}),"instanceName":"1"}),"instanceName":"1"}),"instanceName":"1"});
            var Q84;
            Q84=makeQuery(id+"F8.opPattern","COPY",BODY,{"derivedFrom":makeQuery(id+"F7.opPattern","COPY",BODY,{"derivedFrom":makeQuery(id+"F6.opPattern","COPY",BODY,{"derivedFrom":makeQuery(id+"F1.opRevolve","SWEPT_BODY",BODY,{"disambiguationData":[OSD([sQuery(id+"F0.wireOp",EDGE,"E1")])]}),"instanceName":"1"}),"instanceName":"1"}),"instanceName":"1"});
            var Q85;
            Q85=makeQuery(id+"F8.opPattern","COPY",BODY,{"derivedFrom":makeQuery(id+"F7.opPattern","COPY",BODY,{"derivedFrom":makeQuery(id+"F6.opPattern","COPY",BODY,{"derivedFrom":makeQuery(id+"F2.opPattern","COPY",BODY,{"derivedFrom":makeQuery(id+"F1.opRevolve","SWEPT_BODY",BODY,{"disambiguationData":[OSD([sQuery(id+"F0.wireOp",EDGE,"E1")])]}),"instanceName":"1"}),"instanceName":"1"}),"instanceName":"1"}),"instanceName":"1"});
            var Q86;
            Q86=makeQuery(id+"F8.opPattern","COPY",BODY,{"derivedFrom":makeQuery(id+"F7.opPattern","COPY",BODY,{"derivedFrom":makeQuery(id+"F6.opPattern","COPY",BODY,{"derivedFrom":makeQuery(id+"F3.opPattern","COPY",BODY,{"derivedFrom":makeQuery(id+"F2.opPattern","COPY",BODY,{"derivedFrom":makeQuery(id+"F1.opRevolve","SWEPT_BODY",BODY,{"disambiguationData":[OSD([sQuery(id+"F0.wireOp",EDGE,"E1")])]}),"instanceName":"1"}),"instanceName":"1"}),"instanceName":"1"}),"instanceName":"1"}),"instanceName":"1"});
            var Q87;
            Q87=makeQuery(id+"F8.opPattern","COPY",BODY,{"derivedFrom":makeQuery(id+"F7.opPattern","COPY",BODY,{"derivedFrom":makeQuery(id+"F6.opPattern","COPY",BODY,{"derivedFrom":makeQuery(id+"F4.opPattern","COPY",BODY,{"derivedFrom":makeQuery(id+"F1.opRevolve","SWEPT_BODY",BODY,{"disambiguationData":[OSD([sQuery(id+"F0.wireOp",EDGE,"E1")])]}),"instanceName":"1"}),"instanceName":"1"}),"instanceName":"1"}),"instanceName":"1"});
            var Q88;
            Q88=makeQuery(id+"F8.opPattern","COPY",BODY,{"derivedFrom":makeQuery(id+"F7.opPattern","COPY",BODY,{"derivedFrom":makeQuery(id+"F6.opPattern","COPY",BODY,{"derivedFrom":makeQuery(id+"F4.opPattern","COPY",BODY,{"derivedFrom":makeQuery(id+"F2.opPattern","COPY",BODY,{"derivedFrom":makeQuery(id+"F1.opRevolve","SWEPT_BODY",BODY,{"disambiguationData":[OSD([sQuery(id+"F0.wireOp",EDGE,"E1")])]}),"instanceName":"1"}),"instanceName":"1"}),"instanceName":"1"}),"instanceName":"1"}),"instanceName":"1"});
            var Q89;
            Q89=makeQuery(id+"F8.opPattern","COPY",BODY,{"derivedFrom":makeQuery(id+"F7.opPattern","COPY",BODY,{"derivedFrom":makeQuery(id+"F6.opPattern","COPY",BODY,{"derivedFrom":makeQuery(id+"F4.opPattern","COPY",BODY,{"derivedFrom":makeQuery(id+"F3.opPattern","COPY",BODY,{"derivedFrom":makeQuery(id+"F2.opPattern","COPY",BODY,{"derivedFrom":makeQuery(id+"F1.opRevolve","SWEPT_BODY",BODY,{"disambiguationData":[OSD([sQuery(id+"F0.wireOp",EDGE,"E1")])]}),"instanceName":"1"}),"instanceName":"1"}),"instanceName":"1"}),"instanceName":"1"}),"instanceName":"1"}),"instanceName":"1"});
            var Q90;
            Q90=makeQuery(id+"F8.opPattern","COPY",BODY,{"derivedFrom":makeQuery(id+"F7.opPattern","COPY",BODY,{"derivedFrom":makeQuery(id+"F6.opPattern","COPY",BODY,{"derivedFrom":makeQuery(id+"F5.opPattern","COPY",BODY,{"derivedFrom":makeQuery(id+"F1.opRevolve","SWEPT_BODY",BODY,{"disambiguationData":[OSD([sQuery(id+"F0.wireOp",EDGE,"E1")])]}),"instanceName":"1"}),"instanceName":"1"}),"instanceName":"1"}),"instanceName":"1"});
            var Q91;
            Q91=makeQuery(id+"F8.opPattern","COPY",BODY,{"derivedFrom":makeQuery(id+"F7.opPattern","COPY",BODY,{"derivedFrom":makeQuery(id+"F6.opPattern","COPY",BODY,{"derivedFrom":makeQuery(id+"F5.opPattern","COPY",BODY,{"derivedFrom":makeQuery(id+"F2.opPattern","COPY",BODY,{"derivedFrom":makeQuery(id+"F1.opRevolve","SWEPT_BODY",BODY,{"disambiguationData":[OSD([sQuery(id+"F0.wireOp",EDGE,"E1")])]}),"instanceName":"1"}),"instanceName":"1"}),"instanceName":"1"}),"instanceName":"1"}),"instanceName":"1"});
            var Q92;
            Q92=makeQuery(id+"F8.opPattern","COPY",BODY,{"derivedFrom":makeQuery(id+"F7.opPattern","COPY",BODY,{"derivedFrom":makeQuery(id+"F6.opPattern","COPY",BODY,{"derivedFrom":makeQuery(id+"F5.opPattern","COPY",BODY,{"derivedFrom":makeQuery(id+"F3.opPattern","COPY",BODY,{"derivedFrom":makeQuery(id+"F2.opPattern","COPY",BODY,{"derivedFrom":makeQuery(id+"F1.opRevolve","SWEPT_BODY",BODY,{"disambiguationData":[OSD([sQuery(id+"F0.wireOp",EDGE,"E1")])]}),"instanceName":"1"}),"instanceName":"1"}),"instanceName":"1"}),"instanceName":"1"}),"instanceName":"1"}),"instanceName":"1"});
            var Q93;
            Q93=makeQuery(id+"F8.opPattern","COPY",BODY,{"derivedFrom":makeQuery(id+"F7.opPattern","COPY",BODY,{"derivedFrom":makeQuery(id+"F6.opPattern","COPY",BODY,{"derivedFrom":makeQuery(id+"F5.opPattern","COPY",BODY,{"derivedFrom":makeQuery(id+"F4.opPattern","COPY",BODY,{"derivedFrom":makeQuery(id+"F1.opRevolve","SWEPT_BODY",BODY,{"disambiguationData":[OSD([sQuery(id+"F0.wireOp",EDGE,"E1")])]}),"instanceName":"1"}),"instanceName":"1"}),"instanceName":"1"}),"instanceName":"1"}),"instanceName":"1"});
            var Q94;
            Q94=makeQuery(id+"F8.opPattern","COPY",BODY,{"derivedFrom":makeQuery(id+"F7.opPattern","COPY",BODY,{"derivedFrom":makeQuery(id+"F6.opPattern","COPY",BODY,{"derivedFrom":makeQuery(id+"F5.opPattern","COPY",BODY,{"derivedFrom":makeQuery(id+"F4.opPattern","COPY",BODY,{"derivedFrom":makeQuery(id+"F2.opPattern","COPY",BODY,{"derivedFrom":makeQuery(id+"F1.opRevolve","SWEPT_BODY",BODY,{"disambiguationData":[OSD([sQuery(id+"F0.wireOp",EDGE,"E1")])]}),"instanceName":"1"}),"instanceName":"1"}),"instanceName":"1"}),"instanceName":"1"}),"instanceName":"1"}),"instanceName":"1"});
            var Q95;
            Q95=makeQuery(id+"F8.opPattern","COPY",BODY,{"derivedFrom":makeQuery(id+"F7.opPattern","COPY",BODY,{"derivedFrom":makeQuery(id+"F6.opPattern","COPY",BODY,{"derivedFrom":makeQuery(id+"F5.opPattern","COPY",BODY,{"derivedFrom":makeQuery(id+"F4.opPattern","COPY",BODY,{"derivedFrom":makeQuery(id+"F3.opPattern","COPY",BODY,{"derivedFrom":makeQuery(id+"F2.opPattern","COPY",BODY,{"derivedFrom":makeQuery(id+"F1.opRevolve","SWEPT_BODY",BODY,{"disambiguationData":[OSD([sQuery(id+"F0.wireOp",EDGE,"E1")])]}),"instanceName":"1"}),"instanceName":"1"}),"instanceName":"1"}),"instanceName":"1"}),"instanceName":"1"}),"instanceName":"1"}),"instanceName":"1"});
            var Q96;
            Q96=makeQuery(id+"F9.opPattern","COPY",BODY,{"derivedFrom":makeQuery(id+"F1.opRevolve","SWEPT_BODY",BODY,{"disambiguationData":[OSD([sQuery(id+"F0.wireOp",EDGE,"E1")])]}),"instanceName":"1"});
            var Q97;
            Q97=makeQuery(id+"F9.opPattern","COPY",BODY,{"derivedFrom":makeQuery(id+"F2.opPattern","COPY",BODY,{"derivedFrom":makeQuery(id+"F1.opRevolve","SWEPT_BODY",BODY,{"disambiguationData":[OSD([sQuery(id+"F0.wireOp",EDGE,"E1")])]}),"instanceName":"1"}),"instanceName":"1"});
            var Q98;
            Q98=makeQuery(id+"F9.opPattern","COPY",BODY,{"derivedFrom":makeQuery(id+"F3.opPattern","COPY",BODY,{"derivedFrom":makeQuery(id+"F2.opPattern","COPY",BODY,{"derivedFrom":makeQuery(id+"F1.opRevolve","SWEPT_BODY",BODY,{"disambiguationData":[OSD([sQuery(id+"F0.wireOp",EDGE,"E1")])]}),"instanceName":"1"}),"instanceName":"1"}),"instanceName":"1"});
            var Q99;
            Q99=makeQuery(id+"F9.opPattern","COPY",BODY,{"derivedFrom":makeQuery(id+"F4.opPattern","COPY",BODY,{"derivedFrom":makeQuery(id+"F1.opRevolve","SWEPT_BODY",BODY,{"disambiguationData":[OSD([sQuery(id+"F0.wireOp",EDGE,"E1")])]}),"instanceName":"1"}),"instanceName":"1"});
            var Q100;
            Q100=makeQuery(id+"F9.opPattern","COPY",BODY,{"derivedFrom":makeQuery(id+"F4.opPattern","COPY",BODY,{"derivedFrom":makeQuery(id+"F2.opPattern","COPY",BODY,{"derivedFrom":makeQuery(id+"F1.opRevolve","SWEPT_BODY",BODY,{"disambiguationData":[OSD([sQuery(id+"F0.wireOp",EDGE,"E1")])]}),"instanceName":"1"}),"instanceName":"1"}),"instanceName":"1"});
            var Q101;
            Q101=makeQuery(id+"F9.opPattern","COPY",BODY,{"derivedFrom":makeQuery(id+"F4.opPattern","COPY",BODY,{"derivedFrom":makeQuery(id+"F3.opPattern","COPY",BODY,{"derivedFrom":makeQuery(id+"F2.opPattern","COPY",BODY,{"derivedFrom":makeQuery(id+"F1.opRevolve","SWEPT_BODY",BODY,{"disambiguationData":[OSD([sQuery(id+"F0.wireOp",EDGE,"E1")])]}),"instanceName":"1"}),"instanceName":"1"}),"instanceName":"1"}),"instanceName":"1"});
            var Q102;
            Q102=makeQuery(id+"F9.opPattern","COPY",BODY,{"derivedFrom":makeQuery(id+"F5.opPattern","COPY",BODY,{"derivedFrom":makeQuery(id+"F1.opRevolve","SWEPT_BODY",BODY,{"disambiguationData":[OSD([sQuery(id+"F0.wireOp",EDGE,"E1")])]}),"instanceName":"1"}),"instanceName":"1"});
            var Q103;
            Q103=makeQuery(id+"F9.opPattern","COPY",BODY,{"derivedFrom":makeQuery(id+"F5.opPattern","COPY",BODY,{"derivedFrom":makeQuery(id+"F2.opPattern","COPY",BODY,{"derivedFrom":makeQuery(id+"F1.opRevolve","SWEPT_BODY",BODY,{"disambiguationData":[OSD([sQuery(id+"F0.wireOp",EDGE,"E1")])]}),"instanceName":"1"}),"instanceName":"1"}),"instanceName":"1"});
            var Q104;
            Q104=makeQuery(id+"F9.opPattern","COPY",BODY,{"derivedFrom":makeQuery(id+"F5.opPattern","COPY",BODY,{"derivedFrom":makeQuery(id+"F3.opPattern","COPY",BODY,{"derivedFrom":makeQuery(id+"F2.opPattern","COPY",BODY,{"derivedFrom":makeQuery(id+"F1.opRevolve","SWEPT_BODY",BODY,{"disambiguationData":[OSD([sQuery(id+"F0.wireOp",EDGE,"E1")])]}),"instanceName":"1"}),"instanceName":"1"}),"instanceName":"1"}),"instanceName":"1"});
            var Q105;
            Q105=makeQuery(id+"F9.opPattern","COPY",BODY,{"derivedFrom":makeQuery(id+"F5.opPattern","COPY",BODY,{"derivedFrom":makeQuery(id+"F4.opPattern","COPY",BODY,{"derivedFrom":makeQuery(id+"F1.opRevolve","SWEPT_BODY",BODY,{"disambiguationData":[OSD([sQuery(id+"F0.wireOp",EDGE,"E1")])]}),"instanceName":"1"}),"instanceName":"1"}),"instanceName":"1"});
            var Q106;
            Q106=makeQuery(id+"F9.opPattern","COPY",BODY,{"derivedFrom":makeQuery(id+"F5.opPattern","COPY",BODY,{"derivedFrom":makeQuery(id+"F4.opPattern","COPY",BODY,{"derivedFrom":makeQuery(id+"F2.opPattern","COPY",BODY,{"derivedFrom":makeQuery(id+"F1.opRevolve","SWEPT_BODY",BODY,{"disambiguationData":[OSD([sQuery(id+"F0.wireOp",EDGE,"E1")])]}),"instanceName":"1"}),"instanceName":"1"}),"instanceName":"1"}),"instanceName":"1"});
            var Q107;
            Q107=makeQuery(id+"F9.opPattern","COPY",BODY,{"derivedFrom":makeQuery(id+"F5.opPattern","COPY",BODY,{"derivedFrom":makeQuery(id+"F4.opPattern","COPY",BODY,{"derivedFrom":makeQuery(id+"F3.opPattern","COPY",BODY,{"derivedFrom":makeQuery(id+"F2.opPattern","COPY",BODY,{"derivedFrom":makeQuery(id+"F1.opRevolve","SWEPT_BODY",BODY,{"disambiguationData":[OSD([sQuery(id+"F0.wireOp",EDGE,"E1")])]}),"instanceName":"1"}),"instanceName":"1"}),"instanceName":"1"}),"instanceName":"1"}),"instanceName":"1"});
            var Q108;
            Q108=makeQuery(id+"F9.opPattern","COPY",BODY,{"derivedFrom":makeQuery(id+"F6.opPattern","COPY",BODY,{"derivedFrom":makeQuery(id+"F1.opRevolve","SWEPT_BODY",BODY,{"disambiguationData":[OSD([sQuery(id+"F0.wireOp",EDGE,"E1")])]}),"instanceName":"1"}),"instanceName":"1"});
            var Q109;
            Q109=makeQuery(id+"F9.opPattern","COPY",BODY,{"derivedFrom":makeQuery(id+"F6.opPattern","COPY",BODY,{"derivedFrom":makeQuery(id+"F2.opPattern","COPY",BODY,{"derivedFrom":makeQuery(id+"F1.opRevolve","SWEPT_BODY",BODY,{"disambiguationData":[OSD([sQuery(id+"F0.wireOp",EDGE,"E1")])]}),"instanceName":"1"}),"instanceName":"1"}),"instanceName":"1"});
            var Q110;
            Q110=makeQuery(id+"F9.opPattern","COPY",BODY,{"derivedFrom":makeQuery(id+"F6.opPattern","COPY",BODY,{"derivedFrom":makeQuery(id+"F3.opPattern","COPY",BODY,{"derivedFrom":makeQuery(id+"F2.opPattern","COPY",BODY,{"derivedFrom":makeQuery(id+"F1.opRevolve","SWEPT_BODY",BODY,{"disambiguationData":[OSD([sQuery(id+"F0.wireOp",EDGE,"E1")])]}),"instanceName":"1"}),"instanceName":"1"}),"instanceName":"1"}),"instanceName":"1"});
            var Q111;
            Q111=makeQuery(id+"F9.opPattern","COPY",BODY,{"derivedFrom":makeQuery(id+"F6.opPattern","COPY",BODY,{"derivedFrom":makeQuery(id+"F4.opPattern","COPY",BODY,{"derivedFrom":makeQuery(id+"F1.opRevolve","SWEPT_BODY",BODY,{"disambiguationData":[OSD([sQuery(id+"F0.wireOp",EDGE,"E1")])]}),"instanceName":"1"}),"instanceName":"1"}),"instanceName":"1"});
            var Q112;
            Q112=makeQuery(id+"F9.opPattern","COPY",BODY,{"derivedFrom":makeQuery(id+"F6.opPattern","COPY",BODY,{"derivedFrom":makeQuery(id+"F4.opPattern","COPY",BODY,{"derivedFrom":makeQuery(id+"F2.opPattern","COPY",BODY,{"derivedFrom":makeQuery(id+"F1.opRevolve","SWEPT_BODY",BODY,{"disambiguationData":[OSD([sQuery(id+"F0.wireOp",EDGE,"E1")])]}),"instanceName":"1"}),"instanceName":"1"}),"instanceName":"1"}),"instanceName":"1"});
            var Q113;
            Q113=makeQuery(id+"F9.opPattern","COPY",BODY,{"derivedFrom":makeQuery(id+"F6.opPattern","COPY",BODY,{"derivedFrom":makeQuery(id+"F4.opPattern","COPY",BODY,{"derivedFrom":makeQuery(id+"F3.opPattern","COPY",BODY,{"derivedFrom":makeQuery(id+"F2.opPattern","COPY",BODY,{"derivedFrom":makeQuery(id+"F1.opRevolve","SWEPT_BODY",BODY,{"disambiguationData":[OSD([sQuery(id+"F0.wireOp",EDGE,"E1")])]}),"instanceName":"1"}),"instanceName":"1"}),"instanceName":"1"}),"instanceName":"1"}),"instanceName":"1"});
            var Q114;
            Q114=makeQuery(id+"F9.opPattern","COPY",BODY,{"derivedFrom":makeQuery(id+"F6.opPattern","COPY",BODY,{"derivedFrom":makeQuery(id+"F5.opPattern","COPY",BODY,{"derivedFrom":makeQuery(id+"F1.opRevolve","SWEPT_BODY",BODY,{"disambiguationData":[OSD([sQuery(id+"F0.wireOp",EDGE,"E1")])]}),"instanceName":"1"}),"instanceName":"1"}),"instanceName":"1"});
            var Q115;
            Q115=makeQuery(id+"F9.opPattern","COPY",BODY,{"derivedFrom":makeQuery(id+"F6.opPattern","COPY",BODY,{"derivedFrom":makeQuery(id+"F5.opPattern","COPY",BODY,{"derivedFrom":makeQuery(id+"F2.opPattern","COPY",BODY,{"derivedFrom":makeQuery(id+"F1.opRevolve","SWEPT_BODY",BODY,{"disambiguationData":[OSD([sQuery(id+"F0.wireOp",EDGE,"E1")])]}),"instanceName":"1"}),"instanceName":"1"}),"instanceName":"1"}),"instanceName":"1"});
            var Q116;
            Q116=makeQuery(id+"F9.opPattern","COPY",BODY,{"derivedFrom":makeQuery(id+"F6.opPattern","COPY",BODY,{"derivedFrom":makeQuery(id+"F5.opPattern","COPY",BODY,{"derivedFrom":makeQuery(id+"F3.opPattern","COPY",BODY,{"derivedFrom":makeQuery(id+"F2.opPattern","COPY",BODY,{"derivedFrom":makeQuery(id+"F1.opRevolve","SWEPT_BODY",BODY,{"disambiguationData":[OSD([sQuery(id+"F0.wireOp",EDGE,"E1")])]}),"instanceName":"1"}),"instanceName":"1"}),"instanceName":"1"}),"instanceName":"1"}),"instanceName":"1"});
            var Q117;
            Q117=makeQuery(id+"F9.opPattern","COPY",BODY,{"derivedFrom":makeQuery(id+"F6.opPattern","COPY",BODY,{"derivedFrom":makeQuery(id+"F5.opPattern","COPY",BODY,{"derivedFrom":makeQuery(id+"F4.opPattern","COPY",BODY,{"derivedFrom":makeQuery(id+"F1.opRevolve","SWEPT_BODY",BODY,{"disambiguationData":[OSD([sQuery(id+"F0.wireOp",EDGE,"E1")])]}),"instanceName":"1"}),"instanceName":"1"}),"instanceName":"1"}),"instanceName":"1"});
            var Q118;
            Q118=makeQuery(id+"F9.opPattern","COPY",BODY,{"derivedFrom":makeQuery(id+"F6.opPattern","COPY",BODY,{"derivedFrom":makeQuery(id+"F5.opPattern","COPY",BODY,{"derivedFrom":makeQuery(id+"F4.opPattern","COPY",BODY,{"derivedFrom":makeQuery(id+"F2.opPattern","COPY",BODY,{"derivedFrom":makeQuery(id+"F1.opRevolve","SWEPT_BODY",BODY,{"disambiguationData":[OSD([sQuery(id+"F0.wireOp",EDGE,"E1")])]}),"instanceName":"1"}),"instanceName":"1"}),"instanceName":"1"}),"instanceName":"1"}),"instanceName":"1"});
            var Q119;
            Q119=makeQuery(id+"F9.opPattern","COPY",BODY,{"derivedFrom":makeQuery(id+"F6.opPattern","COPY",BODY,{"derivedFrom":makeQuery(id+"F5.opPattern","COPY",BODY,{"derivedFrom":makeQuery(id+"F4.opPattern","COPY",BODY,{"derivedFrom":makeQuery(id+"F3.opPattern","COPY",BODY,{"derivedFrom":makeQuery(id+"F2.opPattern","COPY",BODY,{"derivedFrom":makeQuery(id+"F1.opRevolve","SWEPT_BODY",BODY,{"disambiguationData":[OSD([sQuery(id+"F0.wireOp",EDGE,"E1")])]}),"instanceName":"1"}),"instanceName":"1"}),"instanceName":"1"}),"instanceName":"1"}),"instanceName":"1"}),"instanceName":"1"});
            var Q120;
            Q120=makeQuery(id+"F9.opPattern","COPY",BODY,{"derivedFrom":makeQuery(id+"F7.opPattern","COPY",BODY,{"derivedFrom":makeQuery(id+"F1.opRevolve","SWEPT_BODY",BODY,{"disambiguationData":[OSD([sQuery(id+"F0.wireOp",EDGE,"E1")])]}),"instanceName":"1"}),"instanceName":"1"});
            var Q121;
            Q121=makeQuery(id+"F9.opPattern","COPY",BODY,{"derivedFrom":makeQuery(id+"F7.opPattern","COPY",BODY,{"derivedFrom":makeQuery(id+"F2.opPattern","COPY",BODY,{"derivedFrom":makeQuery(id+"F1.opRevolve","SWEPT_BODY",BODY,{"disambiguationData":[OSD([sQuery(id+"F0.wireOp",EDGE,"E1")])]}),"instanceName":"1"}),"instanceName":"1"}),"instanceName":"1"});
            var Q122;
            Q122=makeQuery(id+"F9.opPattern","COPY",BODY,{"derivedFrom":makeQuery(id+"F7.opPattern","COPY",BODY,{"derivedFrom":makeQuery(id+"F3.opPattern","COPY",BODY,{"derivedFrom":makeQuery(id+"F2.opPattern","COPY",BODY,{"derivedFrom":makeQuery(id+"F1.opRevolve","SWEPT_BODY",BODY,{"disambiguationData":[OSD([sQuery(id+"F0.wireOp",EDGE,"E1")])]}),"instanceName":"1"}),"instanceName":"1"}),"instanceName":"1"}),"instanceName":"1"});
            var Q123;
            Q123=makeQuery(id+"F9.opPattern","COPY",BODY,{"derivedFrom":makeQuery(id+"F7.opPattern","COPY",BODY,{"derivedFrom":makeQuery(id+"F4.opPattern","COPY",BODY,{"derivedFrom":makeQuery(id+"F1.opRevolve","SWEPT_BODY",BODY,{"disambiguationData":[OSD([sQuery(id+"F0.wireOp",EDGE,"E1")])]}),"instanceName":"1"}),"instanceName":"1"}),"instanceName":"1"});
            var Q124;
            Q124=makeQuery(id+"F9.opPattern","COPY",BODY,{"derivedFrom":makeQuery(id+"F7.opPattern","COPY",BODY,{"derivedFrom":makeQuery(id+"F4.opPattern","COPY",BODY,{"derivedFrom":makeQuery(id+"F2.opPattern","COPY",BODY,{"derivedFrom":makeQuery(id+"F1.opRevolve","SWEPT_BODY",BODY,{"disambiguationData":[OSD([sQuery(id+"F0.wireOp",EDGE,"E1")])]}),"instanceName":"1"}),"instanceName":"1"}),"instanceName":"1"}),"instanceName":"1"});
            var Q125;
            Q125=makeQuery(id+"F9.opPattern","COPY",BODY,{"derivedFrom":makeQuery(id+"F7.opPattern","COPY",BODY,{"derivedFrom":makeQuery(id+"F4.opPattern","COPY",BODY,{"derivedFrom":makeQuery(id+"F3.opPattern","COPY",BODY,{"derivedFrom":makeQuery(id+"F2.opPattern","COPY",BODY,{"derivedFrom":makeQuery(id+"F1.opRevolve","SWEPT_BODY",BODY,{"disambiguationData":[OSD([sQuery(id+"F0.wireOp",EDGE,"E1")])]}),"instanceName":"1"}),"instanceName":"1"}),"instanceName":"1"}),"instanceName":"1"}),"instanceName":"1"});
            var Q126;
            Q126=makeQuery(id+"F9.opPattern","COPY",BODY,{"derivedFrom":makeQuery(id+"F7.opPattern","COPY",BODY,{"derivedFrom":makeQuery(id+"F5.opPattern","COPY",BODY,{"derivedFrom":makeQuery(id+"F1.opRevolve","SWEPT_BODY",BODY,{"disambiguationData":[OSD([sQuery(id+"F0.wireOp",EDGE,"E1")])]}),"instanceName":"1"}),"instanceName":"1"}),"instanceName":"1"});
            var Q127;
            Q127=makeQuery(id+"F9.opPattern","COPY",BODY,{"derivedFrom":makeQuery(id+"F7.opPattern","COPY",BODY,{"derivedFrom":makeQuery(id+"F5.opPattern","COPY",BODY,{"derivedFrom":makeQuery(id+"F2.opPattern","COPY",BODY,{"derivedFrom":makeQuery(id+"F1.opRevolve","SWEPT_BODY",BODY,{"disambiguationData":[OSD([sQuery(id+"F0.wireOp",EDGE,"E1")])]}),"instanceName":"1"}),"instanceName":"1"}),"instanceName":"1"}),"instanceName":"1"});
            var Q128;
            Q128=makeQuery(id+"F9.opPattern","COPY",BODY,{"derivedFrom":makeQuery(id+"F7.opPattern","COPY",BODY,{"derivedFrom":makeQuery(id+"F5.opPattern","COPY",BODY,{"derivedFrom":makeQuery(id+"F3.opPattern","COPY",BODY,{"derivedFrom":makeQuery(id+"F2.opPattern","COPY",BODY,{"derivedFrom":makeQuery(id+"F1.opRevolve","SWEPT_BODY",BODY,{"disambiguationData":[OSD([sQuery(id+"F0.wireOp",EDGE,"E1")])]}),"instanceName":"1"}),"instanceName":"1"}),"instanceName":"1"}),"instanceName":"1"}),"instanceName":"1"});
            var Q129;
            Q129=makeQuery(id+"F9.opPattern","COPY",BODY,{"derivedFrom":makeQuery(id+"F7.opPattern","COPY",BODY,{"derivedFrom":makeQuery(id+"F5.opPattern","COPY",BODY,{"derivedFrom":makeQuery(id+"F4.opPattern","COPY",BODY,{"derivedFrom":makeQuery(id+"F1.opRevolve","SWEPT_BODY",BODY,{"disambiguationData":[OSD([sQuery(id+"F0.wireOp",EDGE,"E1")])]}),"instanceName":"1"}),"instanceName":"1"}),"instanceName":"1"}),"instanceName":"1"});
            var Q130;
            Q130=makeQuery(id+"F9.opPattern","COPY",BODY,{"derivedFrom":makeQuery(id+"F7.opPattern","COPY",BODY,{"derivedFrom":makeQuery(id+"F5.opPattern","COPY",BODY,{"derivedFrom":makeQuery(id+"F4.opPattern","COPY",BODY,{"derivedFrom":makeQuery(id+"F2.opPattern","COPY",BODY,{"derivedFrom":makeQuery(id+"F1.opRevolve","SWEPT_BODY",BODY,{"disambiguationData":[OSD([sQuery(id+"F0.wireOp",EDGE,"E1")])]}),"instanceName":"1"}),"instanceName":"1"}),"instanceName":"1"}),"instanceName":"1"}),"instanceName":"1"});
            var Q131;
            Q131=makeQuery(id+"F9.opPattern","COPY",BODY,{"derivedFrom":makeQuery(id+"F7.opPattern","COPY",BODY,{"derivedFrom":makeQuery(id+"F5.opPattern","COPY",BODY,{"derivedFrom":makeQuery(id+"F4.opPattern","COPY",BODY,{"derivedFrom":makeQuery(id+"F3.opPattern","COPY",BODY,{"derivedFrom":makeQuery(id+"F2.opPattern","COPY",BODY,{"derivedFrom":makeQuery(id+"F1.opRevolve","SWEPT_BODY",BODY,{"disambiguationData":[OSD([sQuery(id+"F0.wireOp",EDGE,"E1")])]}),"instanceName":"1"}),"instanceName":"1"}),"instanceName":"1"}),"instanceName":"1"}),"instanceName":"1"}),"instanceName":"1"});
            var Q132;
            Q132=makeQuery(id+"F9.opPattern","COPY",BODY,{"derivedFrom":makeQuery(id+"F7.opPattern","COPY",BODY,{"derivedFrom":makeQuery(id+"F6.opPattern","COPY",BODY,{"derivedFrom":makeQuery(id+"F1.opRevolve","SWEPT_BODY",BODY,{"disambiguationData":[OSD([sQuery(id+"F0.wireOp",EDGE,"E1")])]}),"instanceName":"1"}),"instanceName":"1"}),"instanceName":"1"});
            var Q133;
            Q133=makeQuery(id+"F9.opPattern","COPY",BODY,{"derivedFrom":makeQuery(id+"F7.opPattern","COPY",BODY,{"derivedFrom":makeQuery(id+"F6.opPattern","COPY",BODY,{"derivedFrom":makeQuery(id+"F2.opPattern","COPY",BODY,{"derivedFrom":makeQuery(id+"F1.opRevolve","SWEPT_BODY",BODY,{"disambiguationData":[OSD([sQuery(id+"F0.wireOp",EDGE,"E1")])]}),"instanceName":"1"}),"instanceName":"1"}),"instanceName":"1"}),"instanceName":"1"});
            var Q134;
            Q134=makeQuery(id+"F9.opPattern","COPY",BODY,{"derivedFrom":makeQuery(id+"F7.opPattern","COPY",BODY,{"derivedFrom":makeQuery(id+"F6.opPattern","COPY",BODY,{"derivedFrom":makeQuery(id+"F3.opPattern","COPY",BODY,{"derivedFrom":makeQuery(id+"F2.opPattern","COPY",BODY,{"derivedFrom":makeQuery(id+"F1.opRevolve","SWEPT_BODY",BODY,{"disambiguationData":[OSD([sQuery(id+"F0.wireOp",EDGE,"E1")])]}),"instanceName":"1"}),"instanceName":"1"}),"instanceName":"1"}),"instanceName":"1"}),"instanceName":"1"});
            var Q135;
            Q135=makeQuery(id+"F9.opPattern","COPY",BODY,{"derivedFrom":makeQuery(id+"F7.opPattern","COPY",BODY,{"derivedFrom":makeQuery(id+"F6.opPattern","COPY",BODY,{"derivedFrom":makeQuery(id+"F4.opPattern","COPY",BODY,{"derivedFrom":makeQuery(id+"F1.opRevolve","SWEPT_BODY",BODY,{"disambiguationData":[OSD([sQuery(id+"F0.wireOp",EDGE,"E1")])]}),"instanceName":"1"}),"instanceName":"1"}),"instanceName":"1"}),"instanceName":"1"});
            var Q136;
            Q136=makeQuery(id+"F9.opPattern","COPY",BODY,{"derivedFrom":makeQuery(id+"F7.opPattern","COPY",BODY,{"derivedFrom":makeQuery(id+"F6.opPattern","COPY",BODY,{"derivedFrom":makeQuery(id+"F4.opPattern","COPY",BODY,{"derivedFrom":makeQuery(id+"F2.opPattern","COPY",BODY,{"derivedFrom":makeQuery(id+"F1.opRevolve","SWEPT_BODY",BODY,{"disambiguationData":[OSD([sQuery(id+"F0.wireOp",EDGE,"E1")])]}),"instanceName":"1"}),"instanceName":"1"}),"instanceName":"1"}),"instanceName":"1"}),"instanceName":"1"});
            var Q137;
            Q137=makeQuery(id+"F9.opPattern","COPY",BODY,{"derivedFrom":makeQuery(id+"F7.opPattern","COPY",BODY,{"derivedFrom":makeQuery(id+"F6.opPattern","COPY",BODY,{"derivedFrom":makeQuery(id+"F4.opPattern","COPY",BODY,{"derivedFrom":makeQuery(id+"F3.opPattern","COPY",BODY,{"derivedFrom":makeQuery(id+"F2.opPattern","COPY",BODY,{"derivedFrom":makeQuery(id+"F1.opRevolve","SWEPT_BODY",BODY,{"disambiguationData":[OSD([sQuery(id+"F0.wireOp",EDGE,"E1")])]}),"instanceName":"1"}),"instanceName":"1"}),"instanceName":"1"}),"instanceName":"1"}),"instanceName":"1"}),"instanceName":"1"});
            var Q138;
            Q138=makeQuery(id+"F9.opPattern","COPY",BODY,{"derivedFrom":makeQuery(id+"F7.opPattern","COPY",BODY,{"derivedFrom":makeQuery(id+"F6.opPattern","COPY",BODY,{"derivedFrom":makeQuery(id+"F5.opPattern","COPY",BODY,{"derivedFrom":makeQuery(id+"F1.opRevolve","SWEPT_BODY",BODY,{"disambiguationData":[OSD([sQuery(id+"F0.wireOp",EDGE,"E1")])]}),"instanceName":"1"}),"instanceName":"1"}),"instanceName":"1"}),"instanceName":"1"});
            var Q139;
            Q139=makeQuery(id+"F9.opPattern","COPY",BODY,{"derivedFrom":makeQuery(id+"F7.opPattern","COPY",BODY,{"derivedFrom":makeQuery(id+"F6.opPattern","COPY",BODY,{"derivedFrom":makeQuery(id+"F5.opPattern","COPY",BODY,{"derivedFrom":makeQuery(id+"F2.opPattern","COPY",BODY,{"derivedFrom":makeQuery(id+"F1.opRevolve","SWEPT_BODY",BODY,{"disambiguationData":[OSD([sQuery(id+"F0.wireOp",EDGE,"E1")])]}),"instanceName":"1"}),"instanceName":"1"}),"instanceName":"1"}),"instanceName":"1"}),"instanceName":"1"});
            var Q140;
            Q140=makeQuery(id+"F9.opPattern","COPY",BODY,{"derivedFrom":makeQuery(id+"F7.opPattern","COPY",BODY,{"derivedFrom":makeQuery(id+"F6.opPattern","COPY",BODY,{"derivedFrom":makeQuery(id+"F5.opPattern","COPY",BODY,{"derivedFrom":makeQuery(id+"F3.opPattern","COPY",BODY,{"derivedFrom":makeQuery(id+"F2.opPattern","COPY",BODY,{"derivedFrom":makeQuery(id+"F1.opRevolve","SWEPT_BODY",BODY,{"disambiguationData":[OSD([sQuery(id+"F0.wireOp",EDGE,"E1")])]}),"instanceName":"1"}),"instanceName":"1"}),"instanceName":"1"}),"instanceName":"1"}),"instanceName":"1"}),"instanceName":"1"});
            var Q141;
            Q141=makeQuery(id+"F9.opPattern","COPY",BODY,{"derivedFrom":makeQuery(id+"F7.opPattern","COPY",BODY,{"derivedFrom":makeQuery(id+"F6.opPattern","COPY",BODY,{"derivedFrom":makeQuery(id+"F5.opPattern","COPY",BODY,{"derivedFrom":makeQuery(id+"F4.opPattern","COPY",BODY,{"derivedFrom":makeQuery(id+"F1.opRevolve","SWEPT_BODY",BODY,{"disambiguationData":[OSD([sQuery(id+"F0.wireOp",EDGE,"E1")])]}),"instanceName":"1"}),"instanceName":"1"}),"instanceName":"1"}),"instanceName":"1"}),"instanceName":"1"});
            var Q142;
            Q142=makeQuery(id+"F9.opPattern","COPY",BODY,{"derivedFrom":makeQuery(id+"F7.opPattern","COPY",BODY,{"derivedFrom":makeQuery(id+"F6.opPattern","COPY",BODY,{"derivedFrom":makeQuery(id+"F5.opPattern","COPY",BODY,{"derivedFrom":makeQuery(id+"F4.opPattern","COPY",BODY,{"derivedFrom":makeQuery(id+"F2.opPattern","COPY",BODY,{"derivedFrom":makeQuery(id+"F1.opRevolve","SWEPT_BODY",BODY,{"disambiguationData":[OSD([sQuery(id+"F0.wireOp",EDGE,"E1")])]}),"instanceName":"1"}),"instanceName":"1"}),"instanceName":"1"}),"instanceName":"1"}),"instanceName":"1"}),"instanceName":"1"});
            var Q143;
            Q143=makeQuery(id+"F9.opPattern","COPY",BODY,{"derivedFrom":makeQuery(id+"F7.opPattern","COPY",BODY,{"derivedFrom":makeQuery(id+"F6.opPattern","COPY",BODY,{"derivedFrom":makeQuery(id+"F5.opPattern","COPY",BODY,{"derivedFrom":makeQuery(id+"F4.opPattern","COPY",BODY,{"derivedFrom":makeQuery(id+"F3.opPattern","COPY",BODY,{"derivedFrom":makeQuery(id+"F2.opPattern","COPY",BODY,{"derivedFrom":makeQuery(id+"F1.opRevolve","SWEPT_BODY",BODY,{"disambiguationData":[OSD([sQuery(id+"F0.wireOp",EDGE,"E1")])]}),"instanceName":"1"}),"instanceName":"1"}),"instanceName":"1"}),"instanceName":"1"}),"instanceName":"1"}),"instanceName":"1"}),"instanceName":"1"});
            var Q144;
            Q144=makeQuery(id+"F9.opPattern","COPY",BODY,{"derivedFrom":makeQuery(id+"F8.opPattern","COPY",BODY,{"derivedFrom":makeQuery(id+"F1.opRevolve","SWEPT_BODY",BODY,{"disambiguationData":[OSD([sQuery(id+"F0.wireOp",EDGE,"E1")])]}),"instanceName":"1"}),"instanceName":"1"});
            var Q145;
            Q145=makeQuery(id+"F9.opPattern","COPY",BODY,{"derivedFrom":makeQuery(id+"F8.opPattern","COPY",BODY,{"derivedFrom":makeQuery(id+"F2.opPattern","COPY",BODY,{"derivedFrom":makeQuery(id+"F1.opRevolve","SWEPT_BODY",BODY,{"disambiguationData":[OSD([sQuery(id+"F0.wireOp",EDGE,"E1")])]}),"instanceName":"1"}),"instanceName":"1"}),"instanceName":"1"});
            var Q146;
            Q146=makeQuery(id+"F9.opPattern","COPY",BODY,{"derivedFrom":makeQuery(id+"F8.opPattern","COPY",BODY,{"derivedFrom":makeQuery(id+"F3.opPattern","COPY",BODY,{"derivedFrom":makeQuery(id+"F2.opPattern","COPY",BODY,{"derivedFrom":makeQuery(id+"F1.opRevolve","SWEPT_BODY",BODY,{"disambiguationData":[OSD([sQuery(id+"F0.wireOp",EDGE,"E1")])]}),"instanceName":"1"}),"instanceName":"1"}),"instanceName":"1"}),"instanceName":"1"});
            var Q147;
            Q147=makeQuery(id+"F9.opPattern","COPY",BODY,{"derivedFrom":makeQuery(id+"F8.opPattern","COPY",BODY,{"derivedFrom":makeQuery(id+"F4.opPattern","COPY",BODY,{"derivedFrom":makeQuery(id+"F1.opRevolve","SWEPT_BODY",BODY,{"disambiguationData":[OSD([sQuery(id+"F0.wireOp",EDGE,"E1")])]}),"instanceName":"1"}),"instanceName":"1"}),"instanceName":"1"});
            var Q148;
            Q148=makeQuery(id+"F9.opPattern","COPY",BODY,{"derivedFrom":makeQuery(id+"F8.opPattern","COPY",BODY,{"derivedFrom":makeQuery(id+"F4.opPattern","COPY",BODY,{"derivedFrom":makeQuery(id+"F2.opPattern","COPY",BODY,{"derivedFrom":makeQuery(id+"F1.opRevolve","SWEPT_BODY",BODY,{"disambiguationData":[OSD([sQuery(id+"F0.wireOp",EDGE,"E1")])]}),"instanceName":"1"}),"instanceName":"1"}),"instanceName":"1"}),"instanceName":"1"});
            var Q149;
            Q149=makeQuery(id+"F9.opPattern","COPY",BODY,{"derivedFrom":makeQuery(id+"F8.opPattern","COPY",BODY,{"derivedFrom":makeQuery(id+"F4.opPattern","COPY",BODY,{"derivedFrom":makeQuery(id+"F3.opPattern","COPY",BODY,{"derivedFrom":makeQuery(id+"F2.opPattern","COPY",BODY,{"derivedFrom":makeQuery(id+"F1.opRevolve","SWEPT_BODY",BODY,{"disambiguationData":[OSD([sQuery(id+"F0.wireOp",EDGE,"E1")])]}),"instanceName":"1"}),"instanceName":"1"}),"instanceName":"1"}),"instanceName":"1"}),"instanceName":"1"});
            var Q150;
            Q150=makeQuery(id+"F9.opPattern","COPY",BODY,{"derivedFrom":makeQuery(id+"F8.opPattern","COPY",BODY,{"derivedFrom":makeQuery(id+"F5.opPattern","COPY",BODY,{"derivedFrom":makeQuery(id+"F1.opRevolve","SWEPT_BODY",BODY,{"disambiguationData":[OSD([sQuery(id+"F0.wireOp",EDGE,"E1")])]}),"instanceName":"1"}),"instanceName":"1"}),"instanceName":"1"});
            var Q151;
            Q151=makeQuery(id+"F9.opPattern","COPY",BODY,{"derivedFrom":makeQuery(id+"F8.opPattern","COPY",BODY,{"derivedFrom":makeQuery(id+"F5.opPattern","COPY",BODY,{"derivedFrom":makeQuery(id+"F2.opPattern","COPY",BODY,{"derivedFrom":makeQuery(id+"F1.opRevolve","SWEPT_BODY",BODY,{"disambiguationData":[OSD([sQuery(id+"F0.wireOp",EDGE,"E1")])]}),"instanceName":"1"}),"instanceName":"1"}),"instanceName":"1"}),"instanceName":"1"});
            var Q152;
            Q152=makeQuery(id+"F9.opPattern","COPY",BODY,{"derivedFrom":makeQuery(id+"F8.opPattern","COPY",BODY,{"derivedFrom":makeQuery(id+"F5.opPattern","COPY",BODY,{"derivedFrom":makeQuery(id+"F3.opPattern","COPY",BODY,{"derivedFrom":makeQuery(id+"F2.opPattern","COPY",BODY,{"derivedFrom":makeQuery(id+"F1.opRevolve","SWEPT_BODY",BODY,{"disambiguationData":[OSD([sQuery(id+"F0.wireOp",EDGE,"E1")])]}),"instanceName":"1"}),"instanceName":"1"}),"instanceName":"1"}),"instanceName":"1"}),"instanceName":"1"});
            var Q153;
            Q153=makeQuery(id+"F9.opPattern","COPY",BODY,{"derivedFrom":makeQuery(id+"F8.opPattern","COPY",BODY,{"derivedFrom":makeQuery(id+"F5.opPattern","COPY",BODY,{"derivedFrom":makeQuery(id+"F4.opPattern","COPY",BODY,{"derivedFrom":makeQuery(id+"F1.opRevolve","SWEPT_BODY",BODY,{"disambiguationData":[OSD([sQuery(id+"F0.wireOp",EDGE,"E1")])]}),"instanceName":"1"}),"instanceName":"1"}),"instanceName":"1"}),"instanceName":"1"});
            var Q154;
            Q154=makeQuery(id+"F9.opPattern","COPY",BODY,{"derivedFrom":makeQuery(id+"F8.opPattern","COPY",BODY,{"derivedFrom":makeQuery(id+"F5.opPattern","COPY",BODY,{"derivedFrom":makeQuery(id+"F4.opPattern","COPY",BODY,{"derivedFrom":makeQuery(id+"F2.opPattern","COPY",BODY,{"derivedFrom":makeQuery(id+"F1.opRevolve","SWEPT_BODY",BODY,{"disambiguationData":[OSD([sQuery(id+"F0.wireOp",EDGE,"E1")])]}),"instanceName":"1"}),"instanceName":"1"}),"instanceName":"1"}),"instanceName":"1"}),"instanceName":"1"});
            var Q155;
            Q155=makeQuery(id+"F9.opPattern","COPY",BODY,{"derivedFrom":makeQuery(id+"F8.opPattern","COPY",BODY,{"derivedFrom":makeQuery(id+"F5.opPattern","COPY",BODY,{"derivedFrom":makeQuery(id+"F4.opPattern","COPY",BODY,{"derivedFrom":makeQuery(id+"F3.opPattern","COPY",BODY,{"derivedFrom":makeQuery(id+"F2.opPattern","COPY",BODY,{"derivedFrom":makeQuery(id+"F1.opRevolve","SWEPT_BODY",BODY,{"disambiguationData":[OSD([sQuery(id+"F0.wireOp",EDGE,"E1")])]}),"instanceName":"1"}),"instanceName":"1"}),"instanceName":"1"}),"instanceName":"1"}),"instanceName":"1"}),"instanceName":"1"});
            var Q156;
            Q156=makeQuery(id+"F9.opPattern","COPY",BODY,{"derivedFrom":makeQuery(id+"F8.opPattern","COPY",BODY,{"derivedFrom":makeQuery(id+"F6.opPattern","COPY",BODY,{"derivedFrom":makeQuery(id+"F1.opRevolve","SWEPT_BODY",BODY,{"disambiguationData":[OSD([sQuery(id+"F0.wireOp",EDGE,"E1")])]}),"instanceName":"1"}),"instanceName":"1"}),"instanceName":"1"});
            var Q157;
            Q157=makeQuery(id+"F9.opPattern","COPY",BODY,{"derivedFrom":makeQuery(id+"F8.opPattern","COPY",BODY,{"derivedFrom":makeQuery(id+"F6.opPattern","COPY",BODY,{"derivedFrom":makeQuery(id+"F2.opPattern","COPY",BODY,{"derivedFrom":makeQuery(id+"F1.opRevolve","SWEPT_BODY",BODY,{"disambiguationData":[OSD([sQuery(id+"F0.wireOp",EDGE,"E1")])]}),"instanceName":"1"}),"instanceName":"1"}),"instanceName":"1"}),"instanceName":"1"});
            var Q158;
            Q158=makeQuery(id+"F9.opPattern","COPY",BODY,{"derivedFrom":makeQuery(id+"F8.opPattern","COPY",BODY,{"derivedFrom":makeQuery(id+"F6.opPattern","COPY",BODY,{"derivedFrom":makeQuery(id+"F3.opPattern","COPY",BODY,{"derivedFrom":makeQuery(id+"F2.opPattern","COPY",BODY,{"derivedFrom":makeQuery(id+"F1.opRevolve","SWEPT_BODY",BODY,{"disambiguationData":[OSD([sQuery(id+"F0.wireOp",EDGE,"E1")])]}),"instanceName":"1"}),"instanceName":"1"}),"instanceName":"1"}),"instanceName":"1"}),"instanceName":"1"});
            var Q159;
            Q159=makeQuery(id+"F9.opPattern","COPY",BODY,{"derivedFrom":makeQuery(id+"F8.opPattern","COPY",BODY,{"derivedFrom":makeQuery(id+"F6.opPattern","COPY",BODY,{"derivedFrom":makeQuery(id+"F4.opPattern","COPY",BODY,{"derivedFrom":makeQuery(id+"F1.opRevolve","SWEPT_BODY",BODY,{"disambiguationData":[OSD([sQuery(id+"F0.wireOp",EDGE,"E1")])]}),"instanceName":"1"}),"instanceName":"1"}),"instanceName":"1"}),"instanceName":"1"});
            var Q160;
            Q160=makeQuery(id+"F9.opPattern","COPY",BODY,{"derivedFrom":makeQuery(id+"F8.opPattern","COPY",BODY,{"derivedFrom":makeQuery(id+"F6.opPattern","COPY",BODY,{"derivedFrom":makeQuery(id+"F4.opPattern","COPY",BODY,{"derivedFrom":makeQuery(id+"F2.opPattern","COPY",BODY,{"derivedFrom":makeQuery(id+"F1.opRevolve","SWEPT_BODY",BODY,{"disambiguationData":[OSD([sQuery(id+"F0.wireOp",EDGE,"E1")])]}),"instanceName":"1"}),"instanceName":"1"}),"instanceName":"1"}),"instanceName":"1"}),"instanceName":"1"});
            var Q161;
            Q161=makeQuery(id+"F9.opPattern","COPY",BODY,{"derivedFrom":makeQuery(id+"F8.opPattern","COPY",BODY,{"derivedFrom":makeQuery(id+"F6.opPattern","COPY",BODY,{"derivedFrom":makeQuery(id+"F4.opPattern","COPY",BODY,{"derivedFrom":makeQuery(id+"F3.opPattern","COPY",BODY,{"derivedFrom":makeQuery(id+"F2.opPattern","COPY",BODY,{"derivedFrom":makeQuery(id+"F1.opRevolve","SWEPT_BODY",BODY,{"disambiguationData":[OSD([sQuery(id+"F0.wireOp",EDGE,"E1")])]}),"instanceName":"1"}),"instanceName":"1"}),"instanceName":"1"}),"instanceName":"1"}),"instanceName":"1"}),"instanceName":"1"});
            var Q162;
            Q162=makeQuery(id+"F9.opPattern","COPY",BODY,{"derivedFrom":makeQuery(id+"F8.opPattern","COPY",BODY,{"derivedFrom":makeQuery(id+"F6.opPattern","COPY",BODY,{"derivedFrom":makeQuery(id+"F5.opPattern","COPY",BODY,{"derivedFrom":makeQuery(id+"F1.opRevolve","SWEPT_BODY",BODY,{"disambiguationData":[OSD([sQuery(id+"F0.wireOp",EDGE,"E1")])]}),"instanceName":"1"}),"instanceName":"1"}),"instanceName":"1"}),"instanceName":"1"});
            var Q163;
            Q163=makeQuery(id+"F9.opPattern","COPY",BODY,{"derivedFrom":makeQuery(id+"F8.opPattern","COPY",BODY,{"derivedFrom":makeQuery(id+"F6.opPattern","COPY",BODY,{"derivedFrom":makeQuery(id+"F5.opPattern","COPY",BODY,{"derivedFrom":makeQuery(id+"F2.opPattern","COPY",BODY,{"derivedFrom":makeQuery(id+"F1.opRevolve","SWEPT_BODY",BODY,{"disambiguationData":[OSD([sQuery(id+"F0.wireOp",EDGE,"E1")])]}),"instanceName":"1"}),"instanceName":"1"}),"instanceName":"1"}),"instanceName":"1"}),"instanceName":"1"});
            var Q164;
            Q164=makeQuery(id+"F9.opPattern","COPY",BODY,{"derivedFrom":makeQuery(id+"F8.opPattern","COPY",BODY,{"derivedFrom":makeQuery(id+"F6.opPattern","COPY",BODY,{"derivedFrom":makeQuery(id+"F5.opPattern","COPY",BODY,{"derivedFrom":makeQuery(id+"F3.opPattern","COPY",BODY,{"derivedFrom":makeQuery(id+"F2.opPattern","COPY",BODY,{"derivedFrom":makeQuery(id+"F1.opRevolve","SWEPT_BODY",BODY,{"disambiguationData":[OSD([sQuery(id+"F0.wireOp",EDGE,"E1")])]}),"instanceName":"1"}),"instanceName":"1"}),"instanceName":"1"}),"instanceName":"1"}),"instanceName":"1"}),"instanceName":"1"});
            var Q165;
            Q165=makeQuery(id+"F9.opPattern","COPY",BODY,{"derivedFrom":makeQuery(id+"F8.opPattern","COPY",BODY,{"derivedFrom":makeQuery(id+"F6.opPattern","COPY",BODY,{"derivedFrom":makeQuery(id+"F5.opPattern","COPY",BODY,{"derivedFrom":makeQuery(id+"F4.opPattern","COPY",BODY,{"derivedFrom":makeQuery(id+"F1.opRevolve","SWEPT_BODY",BODY,{"disambiguationData":[OSD([sQuery(id+"F0.wireOp",EDGE,"E1")])]}),"instanceName":"1"}),"instanceName":"1"}),"instanceName":"1"}),"instanceName":"1"}),"instanceName":"1"});
            var Q166;
            Q166=makeQuery(id+"F9.opPattern","COPY",BODY,{"derivedFrom":makeQuery(id+"F8.opPattern","COPY",BODY,{"derivedFrom":makeQuery(id+"F6.opPattern","COPY",BODY,{"derivedFrom":makeQuery(id+"F5.opPattern","COPY",BODY,{"derivedFrom":makeQuery(id+"F4.opPattern","COPY",BODY,{"derivedFrom":makeQuery(id+"F2.opPattern","COPY",BODY,{"derivedFrom":makeQuery(id+"F1.opRevolve","SWEPT_BODY",BODY,{"disambiguationData":[OSD([sQuery(id+"F0.wireOp",EDGE,"E1")])]}),"instanceName":"1"}),"instanceName":"1"}),"instanceName":"1"}),"instanceName":"1"}),"instanceName":"1"}),"instanceName":"1"});
            var Q167;
            Q167=makeQuery(id+"F9.opPattern","COPY",BODY,{"derivedFrom":makeQuery(id+"F8.opPattern","COPY",BODY,{"derivedFrom":makeQuery(id+"F6.opPattern","COPY",BODY,{"derivedFrom":makeQuery(id+"F5.opPattern","COPY",BODY,{"derivedFrom":makeQuery(id+"F4.opPattern","COPY",BODY,{"derivedFrom":makeQuery(id+"F3.opPattern","COPY",BODY,{"derivedFrom":makeQuery(id+"F2.opPattern","COPY",BODY,{"derivedFrom":makeQuery(id+"F1.opRevolve","SWEPT_BODY",BODY,{"disambiguationData":[OSD([sQuery(id+"F0.wireOp",EDGE,"E1")])]}),"instanceName":"1"}),"instanceName":"1"}),"instanceName":"1"}),"instanceName":"1"}),"instanceName":"1"}),"instanceName":"1"}),"instanceName":"1"});
            var Q168;
            Q168=makeQuery(id+"F9.opPattern","COPY",BODY,{"derivedFrom":makeQuery(id+"F8.opPattern","COPY",BODY,{"derivedFrom":makeQuery(id+"F7.opPattern","COPY",BODY,{"derivedFrom":makeQuery(id+"F1.opRevolve","SWEPT_BODY",BODY,{"disambiguationData":[OSD([sQuery(id+"F0.wireOp",EDGE,"E1")])]}),"instanceName":"1"}),"instanceName":"1"}),"instanceName":"1"});
            var Q169;
            Q169=makeQuery(id+"F9.opPattern","COPY",BODY,{"derivedFrom":makeQuery(id+"F8.opPattern","COPY",BODY,{"derivedFrom":makeQuery(id+"F7.opPattern","COPY",BODY,{"derivedFrom":makeQuery(id+"F2.opPattern","COPY",BODY,{"derivedFrom":makeQuery(id+"F1.opRevolve","SWEPT_BODY",BODY,{"disambiguationData":[OSD([sQuery(id+"F0.wireOp",EDGE,"E1")])]}),"instanceName":"1"}),"instanceName":"1"}),"instanceName":"1"}),"instanceName":"1"});
            var Q170;
            Q170=makeQuery(id+"F9.opPattern","COPY",BODY,{"derivedFrom":makeQuery(id+"F8.opPattern","COPY",BODY,{"derivedFrom":makeQuery(id+"F7.opPattern","COPY",BODY,{"derivedFrom":makeQuery(id+"F3.opPattern","COPY",BODY,{"derivedFrom":makeQuery(id+"F2.opPattern","COPY",BODY,{"derivedFrom":makeQuery(id+"F1.opRevolve","SWEPT_BODY",BODY,{"disambiguationData":[OSD([sQuery(id+"F0.wireOp",EDGE,"E1")])]}),"instanceName":"1"}),"instanceName":"1"}),"instanceName":"1"}),"instanceName":"1"}),"instanceName":"1"});
            var Q171;
            Q171=makeQuery(id+"F9.opPattern","COPY",BODY,{"derivedFrom":makeQuery(id+"F8.opPattern","COPY",BODY,{"derivedFrom":makeQuery(id+"F7.opPattern","COPY",BODY,{"derivedFrom":makeQuery(id+"F4.opPattern","COPY",BODY,{"derivedFrom":makeQuery(id+"F1.opRevolve","SWEPT_BODY",BODY,{"disambiguationData":[OSD([sQuery(id+"F0.wireOp",EDGE,"E1")])]}),"instanceName":"1"}),"instanceName":"1"}),"instanceName":"1"}),"instanceName":"1"});
            var Q172;
            Q172=makeQuery(id+"F9.opPattern","COPY",BODY,{"derivedFrom":makeQuery(id+"F8.opPattern","COPY",BODY,{"derivedFrom":makeQuery(id+"F7.opPattern","COPY",BODY,{"derivedFrom":makeQuery(id+"F4.opPattern","COPY",BODY,{"derivedFrom":makeQuery(id+"F2.opPattern","COPY",BODY,{"derivedFrom":makeQuery(id+"F1.opRevolve","SWEPT_BODY",BODY,{"disambiguationData":[OSD([sQuery(id+"F0.wireOp",EDGE,"E1")])]}),"instanceName":"1"}),"instanceName":"1"}),"instanceName":"1"}),"instanceName":"1"}),"instanceName":"1"});
            var Q173;
            Q173=makeQuery(id+"F9.opPattern","COPY",BODY,{"derivedFrom":makeQuery(id+"F8.opPattern","COPY",BODY,{"derivedFrom":makeQuery(id+"F7.opPattern","COPY",BODY,{"derivedFrom":makeQuery(id+"F4.opPattern","COPY",BODY,{"derivedFrom":makeQuery(id+"F3.opPattern","COPY",BODY,{"derivedFrom":makeQuery(id+"F2.opPattern","COPY",BODY,{"derivedFrom":makeQuery(id+"F1.opRevolve","SWEPT_BODY",BODY,{"disambiguationData":[OSD([sQuery(id+"F0.wireOp",EDGE,"E1")])]}),"instanceName":"1"}),"instanceName":"1"}),"instanceName":"1"}),"instanceName":"1"}),"instanceName":"1"}),"instanceName":"1"});
            var Q174;
            Q174=makeQuery(id+"F9.opPattern","COPY",BODY,{"derivedFrom":makeQuery(id+"F8.opPattern","COPY",BODY,{"derivedFrom":makeQuery(id+"F7.opPattern","COPY",BODY,{"derivedFrom":makeQuery(id+"F5.opPattern","COPY",BODY,{"derivedFrom":makeQuery(id+"F1.opRevolve","SWEPT_BODY",BODY,{"disambiguationData":[OSD([sQuery(id+"F0.wireOp",EDGE,"E1")])]}),"instanceName":"1"}),"instanceName":"1"}),"instanceName":"1"}),"instanceName":"1"});
            var Q175;
            Q175=makeQuery(id+"F9.opPattern","COPY",BODY,{"derivedFrom":makeQuery(id+"F8.opPattern","COPY",BODY,{"derivedFrom":makeQuery(id+"F7.opPattern","COPY",BODY,{"derivedFrom":makeQuery(id+"F5.opPattern","COPY",BODY,{"derivedFrom":makeQuery(id+"F2.opPattern","COPY",BODY,{"derivedFrom":makeQuery(id+"F1.opRevolve","SWEPT_BODY",BODY,{"disambiguationData":[OSD([sQuery(id+"F0.wireOp",EDGE,"E1")])]}),"instanceName":"1"}),"instanceName":"1"}),"instanceName":"1"}),"instanceName":"1"}),"instanceName":"1"});
            var Q176;
            Q176=makeQuery(id+"F9.opPattern","COPY",BODY,{"derivedFrom":makeQuery(id+"F8.opPattern","COPY",BODY,{"derivedFrom":makeQuery(id+"F7.opPattern","COPY",BODY,{"derivedFrom":makeQuery(id+"F5.opPattern","COPY",BODY,{"derivedFrom":makeQuery(id+"F3.opPattern","COPY",BODY,{"derivedFrom":makeQuery(id+"F2.opPattern","COPY",BODY,{"derivedFrom":makeQuery(id+"F1.opRevolve","SWEPT_BODY",BODY,{"disambiguationData":[OSD([sQuery(id+"F0.wireOp",EDGE,"E1")])]}),"instanceName":"1"}),"instanceName":"1"}),"instanceName":"1"}),"instanceName":"1"}),"instanceName":"1"}),"instanceName":"1"});
            var Q177;
            Q177=makeQuery(id+"F9.opPattern","COPY",BODY,{"derivedFrom":makeQuery(id+"F8.opPattern","COPY",BODY,{"derivedFrom":makeQuery(id+"F7.opPattern","COPY",BODY,{"derivedFrom":makeQuery(id+"F5.opPattern","COPY",BODY,{"derivedFrom":makeQuery(id+"F4.opPattern","COPY",BODY,{"derivedFrom":makeQuery(id+"F1.opRevolve","SWEPT_BODY",BODY,{"disambiguationData":[OSD([sQuery(id+"F0.wireOp",EDGE,"E1")])]}),"instanceName":"1"}),"instanceName":"1"}),"instanceName":"1"}),"instanceName":"1"}),"instanceName":"1"});
            var Q178;
            Q178=makeQuery(id+"F9.opPattern","COPY",BODY,{"derivedFrom":makeQuery(id+"F8.opPattern","COPY",BODY,{"derivedFrom":makeQuery(id+"F7.opPattern","COPY",BODY,{"derivedFrom":makeQuery(id+"F5.opPattern","COPY",BODY,{"derivedFrom":makeQuery(id+"F4.opPattern","COPY",BODY,{"derivedFrom":makeQuery(id+"F2.opPattern","COPY",BODY,{"derivedFrom":makeQuery(id+"F1.opRevolve","SWEPT_BODY",BODY,{"disambiguationData":[OSD([sQuery(id+"F0.wireOp",EDGE,"E1")])]}),"instanceName":"1"}),"instanceName":"1"}),"instanceName":"1"}),"instanceName":"1"}),"instanceName":"1"}),"instanceName":"1"});
            var Q179;
            Q179=makeQuery(id+"F9.opPattern","COPY",BODY,{"derivedFrom":makeQuery(id+"F8.opPattern","COPY",BODY,{"derivedFrom":makeQuery(id+"F7.opPattern","COPY",BODY,{"derivedFrom":makeQuery(id+"F5.opPattern","COPY",BODY,{"derivedFrom":makeQuery(id+"F4.opPattern","COPY",BODY,{"derivedFrom":makeQuery(id+"F3.opPattern","COPY",BODY,{"derivedFrom":makeQuery(id+"F2.opPattern","COPY",BODY,{"derivedFrom":makeQuery(id+"F1.opRevolve","SWEPT_BODY",BODY,{"disambiguationData":[OSD([sQuery(id+"F0.wireOp",EDGE,"E1")])]}),"instanceName":"1"}),"instanceName":"1"}),"instanceName":"1"}),"instanceName":"1"}),"instanceName":"1"}),"instanceName":"1"}),"instanceName":"1"});
            var Q180;
            Q180=makeQuery(id+"F9.opPattern","COPY",BODY,{"derivedFrom":makeQuery(id+"F8.opPattern","COPY",BODY,{"derivedFrom":makeQuery(id+"F7.opPattern","COPY",BODY,{"derivedFrom":makeQuery(id+"F6.opPattern","COPY",BODY,{"derivedFrom":makeQuery(id+"F1.opRevolve","SWEPT_BODY",BODY,{"disambiguationData":[OSD([sQuery(id+"F0.wireOp",EDGE,"E1")])]}),"instanceName":"1"}),"instanceName":"1"}),"instanceName":"1"}),"instanceName":"1"});
            var Q181;
            Q181=makeQuery(id+"F9.opPattern","COPY",BODY,{"derivedFrom":makeQuery(id+"F8.opPattern","COPY",BODY,{"derivedFrom":makeQuery(id+"F7.opPattern","COPY",BODY,{"derivedFrom":makeQuery(id+"F6.opPattern","COPY",BODY,{"derivedFrom":makeQuery(id+"F2.opPattern","COPY",BODY,{"derivedFrom":makeQuery(id+"F1.opRevolve","SWEPT_BODY",BODY,{"disambiguationData":[OSD([sQuery(id+"F0.wireOp",EDGE,"E1")])]}),"instanceName":"1"}),"instanceName":"1"}),"instanceName":"1"}),"instanceName":"1"}),"instanceName":"1"});
            var Q182;
            Q182=makeQuery(id+"F9.opPattern","COPY",BODY,{"derivedFrom":makeQuery(id+"F8.opPattern","COPY",BODY,{"derivedFrom":makeQuery(id+"F7.opPattern","COPY",BODY,{"derivedFrom":makeQuery(id+"F6.opPattern","COPY",BODY,{"derivedFrom":makeQuery(id+"F3.opPattern","COPY",BODY,{"derivedFrom":makeQuery(id+"F2.opPattern","COPY",BODY,{"derivedFrom":makeQuery(id+"F1.opRevolve","SWEPT_BODY",BODY,{"disambiguationData":[OSD([sQuery(id+"F0.wireOp",EDGE,"E1")])]}),"instanceName":"1"}),"instanceName":"1"}),"instanceName":"1"}),"instanceName":"1"}),"instanceName":"1"}),"instanceName":"1"});
            var Q183;
            Q183=makeQuery(id+"F9.opPattern","COPY",BODY,{"derivedFrom":makeQuery(id+"F8.opPattern","COPY",BODY,{"derivedFrom":makeQuery(id+"F7.opPattern","COPY",BODY,{"derivedFrom":makeQuery(id+"F6.opPattern","COPY",BODY,{"derivedFrom":makeQuery(id+"F4.opPattern","COPY",BODY,{"derivedFrom":makeQuery(id+"F1.opRevolve","SWEPT_BODY",BODY,{"disambiguationData":[OSD([sQuery(id+"F0.wireOp",EDGE,"E1")])]}),"instanceName":"1"}),"instanceName":"1"}),"instanceName":"1"}),"instanceName":"1"}),"instanceName":"1"});
            var Q184;
            Q184=makeQuery(id+"F9.opPattern","COPY",BODY,{"derivedFrom":makeQuery(id+"F8.opPattern","COPY",BODY,{"derivedFrom":makeQuery(id+"F7.opPattern","COPY",BODY,{"derivedFrom":makeQuery(id+"F6.opPattern","COPY",BODY,{"derivedFrom":makeQuery(id+"F4.opPattern","COPY",BODY,{"derivedFrom":makeQuery(id+"F2.opPattern","COPY",BODY,{"derivedFrom":makeQuery(id+"F1.opRevolve","SWEPT_BODY",BODY,{"disambiguationData":[OSD([sQuery(id+"F0.wireOp",EDGE,"E1")])]}),"instanceName":"1"}),"instanceName":"1"}),"instanceName":"1"}),"instanceName":"1"}),"instanceName":"1"}),"instanceName":"1"});
            var Q185;
            Q185=makeQuery(id+"F9.opPattern","COPY",BODY,{"derivedFrom":makeQuery(id+"F8.opPattern","COPY",BODY,{"derivedFrom":makeQuery(id+"F7.opPattern","COPY",BODY,{"derivedFrom":makeQuery(id+"F6.opPattern","COPY",BODY,{"derivedFrom":makeQuery(id+"F4.opPattern","COPY",BODY,{"derivedFrom":makeQuery(id+"F3.opPattern","COPY",BODY,{"derivedFrom":makeQuery(id+"F2.opPattern","COPY",BODY,{"derivedFrom":makeQuery(id+"F1.opRevolve","SWEPT_BODY",BODY,{"disambiguationData":[OSD([sQuery(id+"F0.wireOp",EDGE,"E1")])]}),"instanceName":"1"}),"instanceName":"1"}),"instanceName":"1"}),"instanceName":"1"}),"instanceName":"1"}),"instanceName":"1"}),"instanceName":"1"});
            var Q186;
            Q186=makeQuery(id+"F9.opPattern","COPY",BODY,{"derivedFrom":makeQuery(id+"F8.opPattern","COPY",BODY,{"derivedFrom":makeQuery(id+"F7.opPattern","COPY",BODY,{"derivedFrom":makeQuery(id+"F6.opPattern","COPY",BODY,{"derivedFrom":makeQuery(id+"F5.opPattern","COPY",BODY,{"derivedFrom":makeQuery(id+"F1.opRevolve","SWEPT_BODY",BODY,{"disambiguationData":[OSD([sQuery(id+"F0.wireOp",EDGE,"E1")])]}),"instanceName":"1"}),"instanceName":"1"}),"instanceName":"1"}),"instanceName":"1"}),"instanceName":"1"});
            var Q187;
            Q187=makeQuery(id+"F9.opPattern","COPY",BODY,{"derivedFrom":makeQuery(id+"F8.opPattern","COPY",BODY,{"derivedFrom":makeQuery(id+"F7.opPattern","COPY",BODY,{"derivedFrom":makeQuery(id+"F6.opPattern","COPY",BODY,{"derivedFrom":makeQuery(id+"F5.opPattern","COPY",BODY,{"derivedFrom":makeQuery(id+"F2.opPattern","COPY",BODY,{"derivedFrom":makeQuery(id+"F1.opRevolve","SWEPT_BODY",BODY,{"disambiguationData":[OSD([sQuery(id+"F0.wireOp",EDGE,"E1")])]}),"instanceName":"1"}),"instanceName":"1"}),"instanceName":"1"}),"instanceName":"1"}),"instanceName":"1"}),"instanceName":"1"});
            var Q188;
            Q188=makeQuery(id+"F9.opPattern","COPY",BODY,{"derivedFrom":makeQuery(id+"F8.opPattern","COPY",BODY,{"derivedFrom":makeQuery(id+"F7.opPattern","COPY",BODY,{"derivedFrom":makeQuery(id+"F6.opPattern","COPY",BODY,{"derivedFrom":makeQuery(id+"F5.opPattern","COPY",BODY,{"derivedFrom":makeQuery(id+"F3.opPattern","COPY",BODY,{"derivedFrom":makeQuery(id+"F2.opPattern","COPY",BODY,{"derivedFrom":makeQuery(id+"F1.opRevolve","SWEPT_BODY",BODY,{"disambiguationData":[OSD([sQuery(id+"F0.wireOp",EDGE,"E1")])]}),"instanceName":"1"}),"instanceName":"1"}),"instanceName":"1"}),"instanceName":"1"}),"instanceName":"1"}),"instanceName":"1"}),"instanceName":"1"});
            var Q189;
            Q189=makeQuery(id+"F9.opPattern","COPY",BODY,{"derivedFrom":makeQuery(id+"F8.opPattern","COPY",BODY,{"derivedFrom":makeQuery(id+"F7.opPattern","COPY",BODY,{"derivedFrom":makeQuery(id+"F6.opPattern","COPY",BODY,{"derivedFrom":makeQuery(id+"F5.opPattern","COPY",BODY,{"derivedFrom":makeQuery(id+"F4.opPattern","COPY",BODY,{"derivedFrom":makeQuery(id+"F1.opRevolve","SWEPT_BODY",BODY,{"disambiguationData":[OSD([sQuery(id+"F0.wireOp",EDGE,"E1")])]}),"instanceName":"1"}),"instanceName":"1"}),"instanceName":"1"}),"instanceName":"1"}),"instanceName":"1"}),"instanceName":"1"});
            var Q190;
            Q190=makeQuery(id+"F9.opPattern","COPY",BODY,{"derivedFrom":makeQuery(id+"F8.opPattern","COPY",BODY,{"derivedFrom":makeQuery(id+"F7.opPattern","COPY",BODY,{"derivedFrom":makeQuery(id+"F6.opPattern","COPY",BODY,{"derivedFrom":makeQuery(id+"F5.opPattern","COPY",BODY,{"derivedFrom":makeQuery(id+"F4.opPattern","COPY",BODY,{"derivedFrom":makeQuery(id+"F2.opPattern","COPY",BODY,{"derivedFrom":makeQuery(id+"F1.opRevolve","SWEPT_BODY",BODY,{"disambiguationData":[OSD([sQuery(id+"F0.wireOp",EDGE,"E1")])]}),"instanceName":"1"}),"instanceName":"1"}),"instanceName":"1"}),"instanceName":"1"}),"instanceName":"1"}),"instanceName":"1"}),"instanceName":"1"});
            var Q191;
            Q191=makeQuery(id+"F9.opPattern","COPY",BODY,{"derivedFrom":makeQuery(id+"F8.opPattern","COPY",BODY,{"derivedFrom":makeQuery(id+"F7.opPattern","COPY",BODY,{"derivedFrom":makeQuery(id+"F6.opPattern","COPY",BODY,{"derivedFrom":makeQuery(id+"F5.opPattern","COPY",BODY,{"derivedFrom":makeQuery(id+"F4.opPattern","COPY",BODY,{"derivedFrom":makeQuery(id+"F3.opPattern","COPY",BODY,{"derivedFrom":makeQuery(id+"F2.opPattern","COPY",BODY,{"derivedFrom":makeQuery(id+"F1.opRevolve","SWEPT_BODY",BODY,{"disambiguationData":[OSD([sQuery(id+"F0.wireOp",EDGE,"E1")])]}),"instanceName":"1"}),"instanceName":"1"}),"instanceName":"1"}),"instanceName":"1"}),"instanceName":"1"}),"instanceName":"1"}),"instanceName":"1"}),"instanceName":"1"});
            var Q192;
            Q192=makeQuery(id+"F10.opPattern","COPY",BODY,{"derivedFrom":makeQuery(id+"F1.opRevolve","SWEPT_BODY",BODY,{"disambiguationData":[OSD([sQuery(id+"F0.wireOp",EDGE,"E1")])]}),"instanceName":"1"});
            var Q193;
            Q193=makeQuery(id+"F10.opPattern","COPY",BODY,{"derivedFrom":makeQuery(id+"F2.opPattern","COPY",BODY,{"derivedFrom":makeQuery(id+"F1.opRevolve","SWEPT_BODY",BODY,{"disambiguationData":[OSD([sQuery(id+"F0.wireOp",EDGE,"E1")])]}),"instanceName":"1"}),"instanceName":"1"});
            var Q194;
            Q194=makeQuery(id+"F10.opPattern","COPY",BODY,{"derivedFrom":makeQuery(id+"F3.opPattern","COPY",BODY,{"derivedFrom":makeQuery(id+"F2.opPattern","COPY",BODY,{"derivedFrom":makeQuery(id+"F1.opRevolve","SWEPT_BODY",BODY,{"disambiguationData":[OSD([sQuery(id+"F0.wireOp",EDGE,"E1")])]}),"instanceName":"1"}),"instanceName":"1"}),"instanceName":"1"});
            var Q195;
            Q195=makeQuery(id+"F10.opPattern","COPY",BODY,{"derivedFrom":makeQuery(id+"F4.opPattern","COPY",BODY,{"derivedFrom":makeQuery(id+"F1.opRevolve","SWEPT_BODY",BODY,{"disambiguationData":[OSD([sQuery(id+"F0.wireOp",EDGE,"E1")])]}),"instanceName":"1"}),"instanceName":"1"});
            var Q196;
            Q196=makeQuery(id+"F10.opPattern","COPY",BODY,{"derivedFrom":makeQuery(id+"F4.opPattern","COPY",BODY,{"derivedFrom":makeQuery(id+"F2.opPattern","COPY",BODY,{"derivedFrom":makeQuery(id+"F1.opRevolve","SWEPT_BODY",BODY,{"disambiguationData":[OSD([sQuery(id+"F0.wireOp",EDGE,"E1")])]}),"instanceName":"1"}),"instanceName":"1"}),"instanceName":"1"});
            var Q197;
            Q197=makeQuery(id+"F10.opPattern","COPY",BODY,{"derivedFrom":makeQuery(id+"F4.opPattern","COPY",BODY,{"derivedFrom":makeQuery(id+"F3.opPattern","COPY",BODY,{"derivedFrom":makeQuery(id+"F2.opPattern","COPY",BODY,{"derivedFrom":makeQuery(id+"F1.opRevolve","SWEPT_BODY",BODY,{"disambiguationData":[OSD([sQuery(id+"F0.wireOp",EDGE,"E1")])]}),"instanceName":"1"}),"instanceName":"1"}),"instanceName":"1"}),"instanceName":"1"});
            var Q198;
            Q198=makeQuery(id+"F10.opPattern","COPY",BODY,{"derivedFrom":makeQuery(id+"F5.opPattern","COPY",BODY,{"derivedFrom":makeQuery(id+"F1.opRevolve","SWEPT_BODY",BODY,{"disambiguationData":[OSD([sQuery(id+"F0.wireOp",EDGE,"E1")])]}),"instanceName":"1"}),"instanceName":"1"});
            var Q199;
            Q199=makeQuery(id+"F10.opPattern","COPY",BODY,{"derivedFrom":makeQuery(id+"F5.opPattern","COPY",BODY,{"derivedFrom":makeQuery(id+"F2.opPattern","COPY",BODY,{"derivedFrom":makeQuery(id+"F1.opRevolve","SWEPT_BODY",BODY,{"disambiguationData":[OSD([sQuery(id+"F0.wireOp",EDGE,"E1")])]}),"instanceName":"1"}),"instanceName":"1"}),"instanceName":"1"});
            var Q200;
            Q200=makeQuery(id+"F10.opPattern","COPY",BODY,{"derivedFrom":makeQuery(id+"F5.opPattern","COPY",BODY,{"derivedFrom":makeQuery(id+"F3.opPattern","COPY",BODY,{"derivedFrom":makeQuery(id+"F2.opPattern","COPY",BODY,{"derivedFrom":makeQuery(id+"F1.opRevolve","SWEPT_BODY",BODY,{"disambiguationData":[OSD([sQuery(id+"F0.wireOp",EDGE,"E1")])]}),"instanceName":"1"}),"instanceName":"1"}),"instanceName":"1"}),"instanceName":"1"});
            var Q201;
            Q201=makeQuery(id+"F10.opPattern","COPY",BODY,{"derivedFrom":makeQuery(id+"F5.opPattern","COPY",BODY,{"derivedFrom":makeQuery(id+"F4.opPattern","COPY",BODY,{"derivedFrom":makeQuery(id+"F1.opRevolve","SWEPT_BODY",BODY,{"disambiguationData":[OSD([sQuery(id+"F0.wireOp",EDGE,"E1")])]}),"instanceName":"1"}),"instanceName":"1"}),"instanceName":"1"});
            var Q202;
            Q202=makeQuery(id+"F10.opPattern","COPY",BODY,{"derivedFrom":makeQuery(id+"F5.opPattern","COPY",BODY,{"derivedFrom":makeQuery(id+"F4.opPattern","COPY",BODY,{"derivedFrom":makeQuery(id+"F2.opPattern","COPY",BODY,{"derivedFrom":makeQuery(id+"F1.opRevolve","SWEPT_BODY",BODY,{"disambiguationData":[OSD([sQuery(id+"F0.wireOp",EDGE,"E1")])]}),"instanceName":"1"}),"instanceName":"1"}),"instanceName":"1"}),"instanceName":"1"});
            var Q203;
            Q203=makeQuery(id+"F10.opPattern","COPY",BODY,{"derivedFrom":makeQuery(id+"F5.opPattern","COPY",BODY,{"derivedFrom":makeQuery(id+"F4.opPattern","COPY",BODY,{"derivedFrom":makeQuery(id+"F3.opPattern","COPY",BODY,{"derivedFrom":makeQuery(id+"F2.opPattern","COPY",BODY,{"derivedFrom":makeQuery(id+"F1.opRevolve","SWEPT_BODY",BODY,{"disambiguationData":[OSD([sQuery(id+"F0.wireOp",EDGE,"E1")])]}),"instanceName":"1"}),"instanceName":"1"}),"instanceName":"1"}),"instanceName":"1"}),"instanceName":"1"});
            var Q204;
            Q204=makeQuery(id+"F10.opPattern","COPY",BODY,{"derivedFrom":makeQuery(id+"F6.opPattern","COPY",BODY,{"derivedFrom":makeQuery(id+"F1.opRevolve","SWEPT_BODY",BODY,{"disambiguationData":[OSD([sQuery(id+"F0.wireOp",EDGE,"E1")])]}),"instanceName":"1"}),"instanceName":"1"});
            var Q205;
            Q205=makeQuery(id+"F10.opPattern","COPY",BODY,{"derivedFrom":makeQuery(id+"F6.opPattern","COPY",BODY,{"derivedFrom":makeQuery(id+"F2.opPattern","COPY",BODY,{"derivedFrom":makeQuery(id+"F1.opRevolve","SWEPT_BODY",BODY,{"disambiguationData":[OSD([sQuery(id+"F0.wireOp",EDGE,"E1")])]}),"instanceName":"1"}),"instanceName":"1"}),"instanceName":"1"});
            var Q206;
            Q206=makeQuery(id+"F10.opPattern","COPY",BODY,{"derivedFrom":makeQuery(id+"F6.opPattern","COPY",BODY,{"derivedFrom":makeQuery(id+"F3.opPattern","COPY",BODY,{"derivedFrom":makeQuery(id+"F2.opPattern","COPY",BODY,{"derivedFrom":makeQuery(id+"F1.opRevolve","SWEPT_BODY",BODY,{"disambiguationData":[OSD([sQuery(id+"F0.wireOp",EDGE,"E1")])]}),"instanceName":"1"}),"instanceName":"1"}),"instanceName":"1"}),"instanceName":"1"});
            var Q207;
            Q207=makeQuery(id+"F10.opPattern","COPY",BODY,{"derivedFrom":makeQuery(id+"F6.opPattern","COPY",BODY,{"derivedFrom":makeQuery(id+"F4.opPattern","COPY",BODY,{"derivedFrom":makeQuery(id+"F1.opRevolve","SWEPT_BODY",BODY,{"disambiguationData":[OSD([sQuery(id+"F0.wireOp",EDGE,"E1")])]}),"instanceName":"1"}),"instanceName":"1"}),"instanceName":"1"});
            var Q208;
            Q208=makeQuery(id+"F10.opPattern","COPY",BODY,{"derivedFrom":makeQuery(id+"F6.opPattern","COPY",BODY,{"derivedFrom":makeQuery(id+"F4.opPattern","COPY",BODY,{"derivedFrom":makeQuery(id+"F2.opPattern","COPY",BODY,{"derivedFrom":makeQuery(id+"F1.opRevolve","SWEPT_BODY",BODY,{"disambiguationData":[OSD([sQuery(id+"F0.wireOp",EDGE,"E1")])]}),"instanceName":"1"}),"instanceName":"1"}),"instanceName":"1"}),"instanceName":"1"});
            var Q209;
            Q209=makeQuery(id+"F10.opPattern","COPY",BODY,{"derivedFrom":makeQuery(id+"F6.opPattern","COPY",BODY,{"derivedFrom":makeQuery(id+"F4.opPattern","COPY",BODY,{"derivedFrom":makeQuery(id+"F3.opPattern","COPY",BODY,{"derivedFrom":makeQuery(id+"F2.opPattern","COPY",BODY,{"derivedFrom":makeQuery(id+"F1.opRevolve","SWEPT_BODY",BODY,{"disambiguationData":[OSD([sQuery(id+"F0.wireOp",EDGE,"E1")])]}),"instanceName":"1"}),"instanceName":"1"}),"instanceName":"1"}),"instanceName":"1"}),"instanceName":"1"});
            var Q210;
            Q210=makeQuery(id+"F10.opPattern","COPY",BODY,{"derivedFrom":makeQuery(id+"F6.opPattern","COPY",BODY,{"derivedFrom":makeQuery(id+"F5.opPattern","COPY",BODY,{"derivedFrom":makeQuery(id+"F1.opRevolve","SWEPT_BODY",BODY,{"disambiguationData":[OSD([sQuery(id+"F0.wireOp",EDGE,"E1")])]}),"instanceName":"1"}),"instanceName":"1"}),"instanceName":"1"});
            var Q211;
            Q211=makeQuery(id+"F10.opPattern","COPY",BODY,{"derivedFrom":makeQuery(id+"F6.opPattern","COPY",BODY,{"derivedFrom":makeQuery(id+"F5.opPattern","COPY",BODY,{"derivedFrom":makeQuery(id+"F2.opPattern","COPY",BODY,{"derivedFrom":makeQuery(id+"F1.opRevolve","SWEPT_BODY",BODY,{"disambiguationData":[OSD([sQuery(id+"F0.wireOp",EDGE,"E1")])]}),"instanceName":"1"}),"instanceName":"1"}),"instanceName":"1"}),"instanceName":"1"});
            var Q212;
            Q212=makeQuery(id+"F10.opPattern","COPY",BODY,{"derivedFrom":makeQuery(id+"F6.opPattern","COPY",BODY,{"derivedFrom":makeQuery(id+"F5.opPattern","COPY",BODY,{"derivedFrom":makeQuery(id+"F3.opPattern","COPY",BODY,{"derivedFrom":makeQuery(id+"F2.opPattern","COPY",BODY,{"derivedFrom":makeQuery(id+"F1.opRevolve","SWEPT_BODY",BODY,{"disambiguationData":[OSD([sQuery(id+"F0.wireOp",EDGE,"E1")])]}),"instanceName":"1"}),"instanceName":"1"}),"instanceName":"1"}),"instanceName":"1"}),"instanceName":"1"});
            var Q213;
            Q213=makeQuery(id+"F10.opPattern","COPY",BODY,{"derivedFrom":makeQuery(id+"F6.opPattern","COPY",BODY,{"derivedFrom":makeQuery(id+"F5.opPattern","COPY",BODY,{"derivedFrom":makeQuery(id+"F4.opPattern","COPY",BODY,{"derivedFrom":makeQuery(id+"F1.opRevolve","SWEPT_BODY",BODY,{"disambiguationData":[OSD([sQuery(id+"F0.wireOp",EDGE,"E1")])]}),"instanceName":"1"}),"instanceName":"1"}),"instanceName":"1"}),"instanceName":"1"});
            var Q214;
            Q214=makeQuery(id+"F10.opPattern","COPY",BODY,{"derivedFrom":makeQuery(id+"F6.opPattern","COPY",BODY,{"derivedFrom":makeQuery(id+"F5.opPattern","COPY",BODY,{"derivedFrom":makeQuery(id+"F4.opPattern","COPY",BODY,{"derivedFrom":makeQuery(id+"F2.opPattern","COPY",BODY,{"derivedFrom":makeQuery(id+"F1.opRevolve","SWEPT_BODY",BODY,{"disambiguationData":[OSD([sQuery(id+"F0.wireOp",EDGE,"E1")])]}),"instanceName":"1"}),"instanceName":"1"}),"instanceName":"1"}),"instanceName":"1"}),"instanceName":"1"});
            var Q215;
            Q215=makeQuery(id+"F10.opPattern","COPY",BODY,{"derivedFrom":makeQuery(id+"F6.opPattern","COPY",BODY,{"derivedFrom":makeQuery(id+"F5.opPattern","COPY",BODY,{"derivedFrom":makeQuery(id+"F4.opPattern","COPY",BODY,{"derivedFrom":makeQuery(id+"F3.opPattern","COPY",BODY,{"derivedFrom":makeQuery(id+"F2.opPattern","COPY",BODY,{"derivedFrom":makeQuery(id+"F1.opRevolve","SWEPT_BODY",BODY,{"disambiguationData":[OSD([sQuery(id+"F0.wireOp",EDGE,"E1")])]}),"instanceName":"1"}),"instanceName":"1"}),"instanceName":"1"}),"instanceName":"1"}),"instanceName":"1"}),"instanceName":"1"});
            var Q216;
            Q216=makeQuery(id+"F10.opPattern","COPY",BODY,{"derivedFrom":makeQuery(id+"F7.opPattern","COPY",BODY,{"derivedFrom":makeQuery(id+"F1.opRevolve","SWEPT_BODY",BODY,{"disambiguationData":[OSD([sQuery(id+"F0.wireOp",EDGE,"E1")])]}),"instanceName":"1"}),"instanceName":"1"});
            var Q217;
            Q217=makeQuery(id+"F10.opPattern","COPY",BODY,{"derivedFrom":makeQuery(id+"F7.opPattern","COPY",BODY,{"derivedFrom":makeQuery(id+"F2.opPattern","COPY",BODY,{"derivedFrom":makeQuery(id+"F1.opRevolve","SWEPT_BODY",BODY,{"disambiguationData":[OSD([sQuery(id+"F0.wireOp",EDGE,"E1")])]}),"instanceName":"1"}),"instanceName":"1"}),"instanceName":"1"});
            var Q218;
            Q218=makeQuery(id+"F10.opPattern","COPY",BODY,{"derivedFrom":makeQuery(id+"F7.opPattern","COPY",BODY,{"derivedFrom":makeQuery(id+"F3.opPattern","COPY",BODY,{"derivedFrom":makeQuery(id+"F2.opPattern","COPY",BODY,{"derivedFrom":makeQuery(id+"F1.opRevolve","SWEPT_BODY",BODY,{"disambiguationData":[OSD([sQuery(id+"F0.wireOp",EDGE,"E1")])]}),"instanceName":"1"}),"instanceName":"1"}),"instanceName":"1"}),"instanceName":"1"});
            var Q219;
            Q219=makeQuery(id+"F10.opPattern","COPY",BODY,{"derivedFrom":makeQuery(id+"F7.opPattern","COPY",BODY,{"derivedFrom":makeQuery(id+"F4.opPattern","COPY",BODY,{"derivedFrom":makeQuery(id+"F1.opRevolve","SWEPT_BODY",BODY,{"disambiguationData":[OSD([sQuery(id+"F0.wireOp",EDGE,"E1")])]}),"instanceName":"1"}),"instanceName":"1"}),"instanceName":"1"});
            var Q220;
            Q220=makeQuery(id+"F10.opPattern","COPY",BODY,{"derivedFrom":makeQuery(id+"F7.opPattern","COPY",BODY,{"derivedFrom":makeQuery(id+"F4.opPattern","COPY",BODY,{"derivedFrom":makeQuery(id+"F2.opPattern","COPY",BODY,{"derivedFrom":makeQuery(id+"F1.opRevolve","SWEPT_BODY",BODY,{"disambiguationData":[OSD([sQuery(id+"F0.wireOp",EDGE,"E1")])]}),"instanceName":"1"}),"instanceName":"1"}),"instanceName":"1"}),"instanceName":"1"});
            var Q221;
            Q221=makeQuery(id+"F10.opPattern","COPY",BODY,{"derivedFrom":makeQuery(id+"F7.opPattern","COPY",BODY,{"derivedFrom":makeQuery(id+"F4.opPattern","COPY",BODY,{"derivedFrom":makeQuery(id+"F3.opPattern","COPY",BODY,{"derivedFrom":makeQuery(id+"F2.opPattern","COPY",BODY,{"derivedFrom":makeQuery(id+"F1.opRevolve","SWEPT_BODY",BODY,{"disambiguationData":[OSD([sQuery(id+"F0.wireOp",EDGE,"E1")])]}),"instanceName":"1"}),"instanceName":"1"}),"instanceName":"1"}),"instanceName":"1"}),"instanceName":"1"});
            var Q222;
            Q222=makeQuery(id+"F10.opPattern","COPY",BODY,{"derivedFrom":makeQuery(id+"F7.opPattern","COPY",BODY,{"derivedFrom":makeQuery(id+"F5.opPattern","COPY",BODY,{"derivedFrom":makeQuery(id+"F1.opRevolve","SWEPT_BODY",BODY,{"disambiguationData":[OSD([sQuery(id+"F0.wireOp",EDGE,"E1")])]}),"instanceName":"1"}),"instanceName":"1"}),"instanceName":"1"});
            var Q223;
            Q223=makeQuery(id+"F10.opPattern","COPY",BODY,{"derivedFrom":makeQuery(id+"F7.opPattern","COPY",BODY,{"derivedFrom":makeQuery(id+"F5.opPattern","COPY",BODY,{"derivedFrom":makeQuery(id+"F2.opPattern","COPY",BODY,{"derivedFrom":makeQuery(id+"F1.opRevolve","SWEPT_BODY",BODY,{"disambiguationData":[OSD([sQuery(id+"F0.wireOp",EDGE,"E1")])]}),"instanceName":"1"}),"instanceName":"1"}),"instanceName":"1"}),"instanceName":"1"});
            var Q224;
            Q224=makeQuery(id+"F10.opPattern","COPY",BODY,{"derivedFrom":makeQuery(id+"F7.opPattern","COPY",BODY,{"derivedFrom":makeQuery(id+"F5.opPattern","COPY",BODY,{"derivedFrom":makeQuery(id+"F3.opPattern","COPY",BODY,{"derivedFrom":makeQuery(id+"F2.opPattern","COPY",BODY,{"derivedFrom":makeQuery(id+"F1.opRevolve","SWEPT_BODY",BODY,{"disambiguationData":[OSD([sQuery(id+"F0.wireOp",EDGE,"E1")])]}),"instanceName":"1"}),"instanceName":"1"}),"instanceName":"1"}),"instanceName":"1"}),"instanceName":"1"});
            var Q225;
            Q225=makeQuery(id+"F10.opPattern","COPY",BODY,{"derivedFrom":makeQuery(id+"F7.opPattern","COPY",BODY,{"derivedFrom":makeQuery(id+"F5.opPattern","COPY",BODY,{"derivedFrom":makeQuery(id+"F4.opPattern","COPY",BODY,{"derivedFrom":makeQuery(id+"F1.opRevolve","SWEPT_BODY",BODY,{"disambiguationData":[OSD([sQuery(id+"F0.wireOp",EDGE,"E1")])]}),"instanceName":"1"}),"instanceName":"1"}),"instanceName":"1"}),"instanceName":"1"});
            var Q226;
            Q226=makeQuery(id+"F10.opPattern","COPY",BODY,{"derivedFrom":makeQuery(id+"F7.opPattern","COPY",BODY,{"derivedFrom":makeQuery(id+"F5.opPattern","COPY",BODY,{"derivedFrom":makeQuery(id+"F4.opPattern","COPY",BODY,{"derivedFrom":makeQuery(id+"F2.opPattern","COPY",BODY,{"derivedFrom":makeQuery(id+"F1.opRevolve","SWEPT_BODY",BODY,{"disambiguationData":[OSD([sQuery(id+"F0.wireOp",EDGE,"E1")])]}),"instanceName":"1"}),"instanceName":"1"}),"instanceName":"1"}),"instanceName":"1"}),"instanceName":"1"});
            var Q227;
            Q227=makeQuery(id+"F10.opPattern","COPY",BODY,{"derivedFrom":makeQuery(id+"F7.opPattern","COPY",BODY,{"derivedFrom":makeQuery(id+"F5.opPattern","COPY",BODY,{"derivedFrom":makeQuery(id+"F4.opPattern","COPY",BODY,{"derivedFrom":makeQuery(id+"F3.opPattern","COPY",BODY,{"derivedFrom":makeQuery(id+"F2.opPattern","COPY",BODY,{"derivedFrom":makeQuery(id+"F1.opRevolve","SWEPT_BODY",BODY,{"disambiguationData":[OSD([sQuery(id+"F0.wireOp",EDGE,"E1")])]}),"instanceName":"1"}),"instanceName":"1"}),"instanceName":"1"}),"instanceName":"1"}),"instanceName":"1"}),"instanceName":"1"});
            var Q228;
            Q228=makeQuery(id+"F10.opPattern","COPY",BODY,{"derivedFrom":makeQuery(id+"F7.opPattern","COPY",BODY,{"derivedFrom":makeQuery(id+"F6.opPattern","COPY",BODY,{"derivedFrom":makeQuery(id+"F1.opRevolve","SWEPT_BODY",BODY,{"disambiguationData":[OSD([sQuery(id+"F0.wireOp",EDGE,"E1")])]}),"instanceName":"1"}),"instanceName":"1"}),"instanceName":"1"});
            var Q229;
            Q229=makeQuery(id+"F10.opPattern","COPY",BODY,{"derivedFrom":makeQuery(id+"F7.opPattern","COPY",BODY,{"derivedFrom":makeQuery(id+"F6.opPattern","COPY",BODY,{"derivedFrom":makeQuery(id+"F2.opPattern","COPY",BODY,{"derivedFrom":makeQuery(id+"F1.opRevolve","SWEPT_BODY",BODY,{"disambiguationData":[OSD([sQuery(id+"F0.wireOp",EDGE,"E1")])]}),"instanceName":"1"}),"instanceName":"1"}),"instanceName":"1"}),"instanceName":"1"});
            var Q230;
            Q230=makeQuery(id+"F10.opPattern","COPY",BODY,{"derivedFrom":makeQuery(id+"F7.opPattern","COPY",BODY,{"derivedFrom":makeQuery(id+"F6.opPattern","COPY",BODY,{"derivedFrom":makeQuery(id+"F3.opPattern","COPY",BODY,{"derivedFrom":makeQuery(id+"F2.opPattern","COPY",BODY,{"derivedFrom":makeQuery(id+"F1.opRevolve","SWEPT_BODY",BODY,{"disambiguationData":[OSD([sQuery(id+"F0.wireOp",EDGE,"E1")])]}),"instanceName":"1"}),"instanceName":"1"}),"instanceName":"1"}),"instanceName":"1"}),"instanceName":"1"});
            var Q231;
            Q231=makeQuery(id+"F10.opPattern","COPY",BODY,{"derivedFrom":makeQuery(id+"F7.opPattern","COPY",BODY,{"derivedFrom":makeQuery(id+"F6.opPattern","COPY",BODY,{"derivedFrom":makeQuery(id+"F4.opPattern","COPY",BODY,{"derivedFrom":makeQuery(id+"F1.opRevolve","SWEPT_BODY",BODY,{"disambiguationData":[OSD([sQuery(id+"F0.wireOp",EDGE,"E1")])]}),"instanceName":"1"}),"instanceName":"1"}),"instanceName":"1"}),"instanceName":"1"});
            var Q232;
            Q232=makeQuery(id+"F10.opPattern","COPY",BODY,{"derivedFrom":makeQuery(id+"F7.opPattern","COPY",BODY,{"derivedFrom":makeQuery(id+"F6.opPattern","COPY",BODY,{"derivedFrom":makeQuery(id+"F4.opPattern","COPY",BODY,{"derivedFrom":makeQuery(id+"F2.opPattern","COPY",BODY,{"derivedFrom":makeQuery(id+"F1.opRevolve","SWEPT_BODY",BODY,{"disambiguationData":[OSD([sQuery(id+"F0.wireOp",EDGE,"E1")])]}),"instanceName":"1"}),"instanceName":"1"}),"instanceName":"1"}),"instanceName":"1"}),"instanceName":"1"});
            var Q233;
            Q233=makeQuery(id+"F10.opPattern","COPY",BODY,{"derivedFrom":makeQuery(id+"F7.opPattern","COPY",BODY,{"derivedFrom":makeQuery(id+"F6.opPattern","COPY",BODY,{"derivedFrom":makeQuery(id+"F4.opPattern","COPY",BODY,{"derivedFrom":makeQuery(id+"F3.opPattern","COPY",BODY,{"derivedFrom":makeQuery(id+"F2.opPattern","COPY",BODY,{"derivedFrom":makeQuery(id+"F1.opRevolve","SWEPT_BODY",BODY,{"disambiguationData":[OSD([sQuery(id+"F0.wireOp",EDGE,"E1")])]}),"instanceName":"1"}),"instanceName":"1"}),"instanceName":"1"}),"instanceName":"1"}),"instanceName":"1"}),"instanceName":"1"});
            var Q234;
            Q234=makeQuery(id+"F10.opPattern","COPY",BODY,{"derivedFrom":makeQuery(id+"F7.opPattern","COPY",BODY,{"derivedFrom":makeQuery(id+"F6.opPattern","COPY",BODY,{"derivedFrom":makeQuery(id+"F5.opPattern","COPY",BODY,{"derivedFrom":makeQuery(id+"F1.opRevolve","SWEPT_BODY",BODY,{"disambiguationData":[OSD([sQuery(id+"F0.wireOp",EDGE,"E1")])]}),"instanceName":"1"}),"instanceName":"1"}),"instanceName":"1"}),"instanceName":"1"});
            var Q235;
            Q235=makeQuery(id+"F10.opPattern","COPY",BODY,{"derivedFrom":makeQuery(id+"F7.opPattern","COPY",BODY,{"derivedFrom":makeQuery(id+"F6.opPattern","COPY",BODY,{"derivedFrom":makeQuery(id+"F5.opPattern","COPY",BODY,{"derivedFrom":makeQuery(id+"F2.opPattern","COPY",BODY,{"derivedFrom":makeQuery(id+"F1.opRevolve","SWEPT_BODY",BODY,{"disambiguationData":[OSD([sQuery(id+"F0.wireOp",EDGE,"E1")])]}),"instanceName":"1"}),"instanceName":"1"}),"instanceName":"1"}),"instanceName":"1"}),"instanceName":"1"});
            var Q236;
            Q236=makeQuery(id+"F10.opPattern","COPY",BODY,{"derivedFrom":makeQuery(id+"F7.opPattern","COPY",BODY,{"derivedFrom":makeQuery(id+"F6.opPattern","COPY",BODY,{"derivedFrom":makeQuery(id+"F5.opPattern","COPY",BODY,{"derivedFrom":makeQuery(id+"F3.opPattern","COPY",BODY,{"derivedFrom":makeQuery(id+"F2.opPattern","COPY",BODY,{"derivedFrom":makeQuery(id+"F1.opRevolve","SWEPT_BODY",BODY,{"disambiguationData":[OSD([sQuery(id+"F0.wireOp",EDGE,"E1")])]}),"instanceName":"1"}),"instanceName":"1"}),"instanceName":"1"}),"instanceName":"1"}),"instanceName":"1"}),"instanceName":"1"});
            var Q237;
            Q237=makeQuery(id+"F10.opPattern","COPY",BODY,{"derivedFrom":makeQuery(id+"F7.opPattern","COPY",BODY,{"derivedFrom":makeQuery(id+"F6.opPattern","COPY",BODY,{"derivedFrom":makeQuery(id+"F5.opPattern","COPY",BODY,{"derivedFrom":makeQuery(id+"F4.opPattern","COPY",BODY,{"derivedFrom":makeQuery(id+"F1.opRevolve","SWEPT_BODY",BODY,{"disambiguationData":[OSD([sQuery(id+"F0.wireOp",EDGE,"E1")])]}),"instanceName":"1"}),"instanceName":"1"}),"instanceName":"1"}),"instanceName":"1"}),"instanceName":"1"});
            var Q238;
            Q238=makeQuery(id+"F10.opPattern","COPY",BODY,{"derivedFrom":makeQuery(id+"F7.opPattern","COPY",BODY,{"derivedFrom":makeQuery(id+"F6.opPattern","COPY",BODY,{"derivedFrom":makeQuery(id+"F5.opPattern","COPY",BODY,{"derivedFrom":makeQuery(id+"F4.opPattern","COPY",BODY,{"derivedFrom":makeQuery(id+"F2.opPattern","COPY",BODY,{"derivedFrom":makeQuery(id+"F1.opRevolve","SWEPT_BODY",BODY,{"disambiguationData":[OSD([sQuery(id+"F0.wireOp",EDGE,"E1")])]}),"instanceName":"1"}),"instanceName":"1"}),"instanceName":"1"}),"instanceName":"1"}),"instanceName":"1"}),"instanceName":"1"});
            var Q239;
            Q239=makeQuery(id+"F10.opPattern","COPY",BODY,{"derivedFrom":makeQuery(id+"F7.opPattern","COPY",BODY,{"derivedFrom":makeQuery(id+"F6.opPattern","COPY",BODY,{"derivedFrom":makeQuery(id+"F5.opPattern","COPY",BODY,{"derivedFrom":makeQuery(id+"F4.opPattern","COPY",BODY,{"derivedFrom":makeQuery(id+"F3.opPattern","COPY",BODY,{"derivedFrom":makeQuery(id+"F2.opPattern","COPY",BODY,{"derivedFrom":makeQuery(id+"F1.opRevolve","SWEPT_BODY",BODY,{"disambiguationData":[OSD([sQuery(id+"F0.wireOp",EDGE,"E1")])]}),"instanceName":"1"}),"instanceName":"1"}),"instanceName":"1"}),"instanceName":"1"}),"instanceName":"1"}),"instanceName":"1"}),"instanceName":"1"});
            var Q240;
            Q240=makeQuery(id+"F10.opPattern","COPY",BODY,{"derivedFrom":makeQuery(id+"F8.opPattern","COPY",BODY,{"derivedFrom":makeQuery(id+"F1.opRevolve","SWEPT_BODY",BODY,{"disambiguationData":[OSD([sQuery(id+"F0.wireOp",EDGE,"E1")])]}),"instanceName":"1"}),"instanceName":"1"});
            var Q241;
            Q241=makeQuery(id+"F10.opPattern","COPY",BODY,{"derivedFrom":makeQuery(id+"F8.opPattern","COPY",BODY,{"derivedFrom":makeQuery(id+"F2.opPattern","COPY",BODY,{"derivedFrom":makeQuery(id+"F1.opRevolve","SWEPT_BODY",BODY,{"disambiguationData":[OSD([sQuery(id+"F0.wireOp",EDGE,"E1")])]}),"instanceName":"1"}),"instanceName":"1"}),"instanceName":"1"});
            var Q242;
            Q242=makeQuery(id+"F10.opPattern","COPY",BODY,{"derivedFrom":makeQuery(id+"F8.opPattern","COPY",BODY,{"derivedFrom":makeQuery(id+"F3.opPattern","COPY",BODY,{"derivedFrom":makeQuery(id+"F2.opPattern","COPY",BODY,{"derivedFrom":makeQuery(id+"F1.opRevolve","SWEPT_BODY",BODY,{"disambiguationData":[OSD([sQuery(id+"F0.wireOp",EDGE,"E1")])]}),"instanceName":"1"}),"instanceName":"1"}),"instanceName":"1"}),"instanceName":"1"});
            var Q243;
            Q243=makeQuery(id+"F10.opPattern","COPY",BODY,{"derivedFrom":makeQuery(id+"F8.opPattern","COPY",BODY,{"derivedFrom":makeQuery(id+"F4.opPattern","COPY",BODY,{"derivedFrom":makeQuery(id+"F1.opRevolve","SWEPT_BODY",BODY,{"disambiguationData":[OSD([sQuery(id+"F0.wireOp",EDGE,"E1")])]}),"instanceName":"1"}),"instanceName":"1"}),"instanceName":"1"});
            var Q244;
            Q244=makeQuery(id+"F10.opPattern","COPY",BODY,{"derivedFrom":makeQuery(id+"F8.opPattern","COPY",BODY,{"derivedFrom":makeQuery(id+"F4.opPattern","COPY",BODY,{"derivedFrom":makeQuery(id+"F2.opPattern","COPY",BODY,{"derivedFrom":makeQuery(id+"F1.opRevolve","SWEPT_BODY",BODY,{"disambiguationData":[OSD([sQuery(id+"F0.wireOp",EDGE,"E1")])]}),"instanceName":"1"}),"instanceName":"1"}),"instanceName":"1"}),"instanceName":"1"});
            var Q245;
            Q245=makeQuery(id+"F10.opPattern","COPY",BODY,{"derivedFrom":makeQuery(id+"F8.opPattern","COPY",BODY,{"derivedFrom":makeQuery(id+"F4.opPattern","COPY",BODY,{"derivedFrom":makeQuery(id+"F3.opPattern","COPY",BODY,{"derivedFrom":makeQuery(id+"F2.opPattern","COPY",BODY,{"derivedFrom":makeQuery(id+"F1.opRevolve","SWEPT_BODY",BODY,{"disambiguationData":[OSD([sQuery(id+"F0.wireOp",EDGE,"E1")])]}),"instanceName":"1"}),"instanceName":"1"}),"instanceName":"1"}),"instanceName":"1"}),"instanceName":"1"});
            var Q246;
            Q246=makeQuery(id+"F10.opPattern","COPY",BODY,{"derivedFrom":makeQuery(id+"F8.opPattern","COPY",BODY,{"derivedFrom":makeQuery(id+"F5.opPattern","COPY",BODY,{"derivedFrom":makeQuery(id+"F1.opRevolve","SWEPT_BODY",BODY,{"disambiguationData":[OSD([sQuery(id+"F0.wireOp",EDGE,"E1")])]}),"instanceName":"1"}),"instanceName":"1"}),"instanceName":"1"});
            var Q247;
            Q247=makeQuery(id+"F10.opPattern","COPY",BODY,{"derivedFrom":makeQuery(id+"F8.opPattern","COPY",BODY,{"derivedFrom":makeQuery(id+"F5.opPattern","COPY",BODY,{"derivedFrom":makeQuery(id+"F2.opPattern","COPY",BODY,{"derivedFrom":makeQuery(id+"F1.opRevolve","SWEPT_BODY",BODY,{"disambiguationData":[OSD([sQuery(id+"F0.wireOp",EDGE,"E1")])]}),"instanceName":"1"}),"instanceName":"1"}),"instanceName":"1"}),"instanceName":"1"});
            var Q248;
            Q248=makeQuery(id+"F10.opPattern","COPY",BODY,{"derivedFrom":makeQuery(id+"F8.opPattern","COPY",BODY,{"derivedFrom":makeQuery(id+"F5.opPattern","COPY",BODY,{"derivedFrom":makeQuery(id+"F3.opPattern","COPY",BODY,{"derivedFrom":makeQuery(id+"F2.opPattern","COPY",BODY,{"derivedFrom":makeQuery(id+"F1.opRevolve","SWEPT_BODY",BODY,{"disambiguationData":[OSD([sQuery(id+"F0.wireOp",EDGE,"E1")])]}),"instanceName":"1"}),"instanceName":"1"}),"instanceName":"1"}),"instanceName":"1"}),"instanceName":"1"});
            var Q249;
            Q249=makeQuery(id+"F10.opPattern","COPY",BODY,{"derivedFrom":makeQuery(id+"F8.opPattern","COPY",BODY,{"derivedFrom":makeQuery(id+"F5.opPattern","COPY",BODY,{"derivedFrom":makeQuery(id+"F4.opPattern","COPY",BODY,{"derivedFrom":makeQuery(id+"F1.opRevolve","SWEPT_BODY",BODY,{"disambiguationData":[OSD([sQuery(id+"F0.wireOp",EDGE,"E1")])]}),"instanceName":"1"}),"instanceName":"1"}),"instanceName":"1"}),"instanceName":"1"});
            var Q250;
            Q250=makeQuery(id+"F10.opPattern","COPY",BODY,{"derivedFrom":makeQuery(id+"F8.opPattern","COPY",BODY,{"derivedFrom":makeQuery(id+"F5.opPattern","COPY",BODY,{"derivedFrom":makeQuery(id+"F4.opPattern","COPY",BODY,{"derivedFrom":makeQuery(id+"F2.opPattern","COPY",BODY,{"derivedFrom":makeQuery(id+"F1.opRevolve","SWEPT_BODY",BODY,{"disambiguationData":[OSD([sQuery(id+"F0.wireOp",EDGE,"E1")])]}),"instanceName":"1"}),"instanceName":"1"}),"instanceName":"1"}),"instanceName":"1"}),"instanceName":"1"});
            var Q251;
            Q251=makeQuery(id+"F10.opPattern","COPY",BODY,{"derivedFrom":makeQuery(id+"F8.opPattern","COPY",BODY,{"derivedFrom":makeQuery(id+"F5.opPattern","COPY",BODY,{"derivedFrom":makeQuery(id+"F4.opPattern","COPY",BODY,{"derivedFrom":makeQuery(id+"F3.opPattern","COPY",BODY,{"derivedFrom":makeQuery(id+"F2.opPattern","COPY",BODY,{"derivedFrom":makeQuery(id+"F1.opRevolve","SWEPT_BODY",BODY,{"disambiguationData":[OSD([sQuery(id+"F0.wireOp",EDGE,"E1")])]}),"instanceName":"1"}),"instanceName":"1"}),"instanceName":"1"}),"instanceName":"1"}),"instanceName":"1"}),"instanceName":"1"});
            var Q252;
            Q252=makeQuery(id+"F10.opPattern","COPY",BODY,{"derivedFrom":makeQuery(id+"F8.opPattern","COPY",BODY,{"derivedFrom":makeQuery(id+"F6.opPattern","COPY",BODY,{"derivedFrom":makeQuery(id+"F1.opRevolve","SWEPT_BODY",BODY,{"disambiguationData":[OSD([sQuery(id+"F0.wireOp",EDGE,"E1")])]}),"instanceName":"1"}),"instanceName":"1"}),"instanceName":"1"});
            var Q253;
            Q253=makeQuery(id+"F10.opPattern","COPY",BODY,{"derivedFrom":makeQuery(id+"F8.opPattern","COPY",BODY,{"derivedFrom":makeQuery(id+"F6.opPattern","COPY",BODY,{"derivedFrom":makeQuery(id+"F2.opPattern","COPY",BODY,{"derivedFrom":makeQuery(id+"F1.opRevolve","SWEPT_BODY",BODY,{"disambiguationData":[OSD([sQuery(id+"F0.wireOp",EDGE,"E1")])]}),"instanceName":"1"}),"instanceName":"1"}),"instanceName":"1"}),"instanceName":"1"});
            var Q254;
            Q254=makeQuery(id+"F10.opPattern","COPY",BODY,{"derivedFrom":makeQuery(id+"F8.opPattern","COPY",BODY,{"derivedFrom":makeQuery(id+"F6.opPattern","COPY",BODY,{"derivedFrom":makeQuery(id+"F3.opPattern","COPY",BODY,{"derivedFrom":makeQuery(id+"F2.opPattern","COPY",BODY,{"derivedFrom":makeQuery(id+"F1.opRevolve","SWEPT_BODY",BODY,{"disambiguationData":[OSD([sQuery(id+"F0.wireOp",EDGE,"E1")])]}),"instanceName":"1"}),"instanceName":"1"}),"instanceName":"1"}),"instanceName":"1"}),"instanceName":"1"});
            var Q255;
            Q255=makeQuery(id+"F10.opPattern","COPY",BODY,{"derivedFrom":makeQuery(id+"F8.opPattern","COPY",BODY,{"derivedFrom":makeQuery(id+"F6.opPattern","COPY",BODY,{"derivedFrom":makeQuery(id+"F4.opPattern","COPY",BODY,{"derivedFrom":makeQuery(id+"F1.opRevolve","SWEPT_BODY",BODY,{"disambiguationData":[OSD([sQuery(id+"F0.wireOp",EDGE,"E1")])]}),"instanceName":"1"}),"instanceName":"1"}),"instanceName":"1"}),"instanceName":"1"});
            var Q256;
            Q256=makeQuery(id+"F10.opPattern","COPY",BODY,{"derivedFrom":makeQuery(id+"F8.opPattern","COPY",BODY,{"derivedFrom":makeQuery(id+"F6.opPattern","COPY",BODY,{"derivedFrom":makeQuery(id+"F4.opPattern","COPY",BODY,{"derivedFrom":makeQuery(id+"F2.opPattern","COPY",BODY,{"derivedFrom":makeQuery(id+"F1.opRevolve","SWEPT_BODY",BODY,{"disambiguationData":[OSD([sQuery(id+"F0.wireOp",EDGE,"E1")])]}),"instanceName":"1"}),"instanceName":"1"}),"instanceName":"1"}),"instanceName":"1"}),"instanceName":"1"});
            var Q257;
            Q257=makeQuery(id+"F10.opPattern","COPY",BODY,{"derivedFrom":makeQuery(id+"F8.opPattern","COPY",BODY,{"derivedFrom":makeQuery(id+"F6.opPattern","COPY",BODY,{"derivedFrom":makeQuery(id+"F4.opPattern","COPY",BODY,{"derivedFrom":makeQuery(id+"F3.opPattern","COPY",BODY,{"derivedFrom":makeQuery(id+"F2.opPattern","COPY",BODY,{"derivedFrom":makeQuery(id+"F1.opRevolve","SWEPT_BODY",BODY,{"disambiguationData":[OSD([sQuery(id+"F0.wireOp",EDGE,"E1")])]}),"instanceName":"1"}),"instanceName":"1"}),"instanceName":"1"}),"instanceName":"1"}),"instanceName":"1"}),"instanceName":"1"});
            var Q258;
            Q258=makeQuery(id+"F10.opPattern","COPY",BODY,{"derivedFrom":makeQuery(id+"F8.opPattern","COPY",BODY,{"derivedFrom":makeQuery(id+"F6.opPattern","COPY",BODY,{"derivedFrom":makeQuery(id+"F5.opPattern","COPY",BODY,{"derivedFrom":makeQuery(id+"F1.opRevolve","SWEPT_BODY",BODY,{"disambiguationData":[OSD([sQuery(id+"F0.wireOp",EDGE,"E1")])]}),"instanceName":"1"}),"instanceName":"1"}),"instanceName":"1"}),"instanceName":"1"});
            var Q259;
            Q259=makeQuery(id+"F10.opPattern","COPY",BODY,{"derivedFrom":makeQuery(id+"F8.opPattern","COPY",BODY,{"derivedFrom":makeQuery(id+"F6.opPattern","COPY",BODY,{"derivedFrom":makeQuery(id+"F5.opPattern","COPY",BODY,{"derivedFrom":makeQuery(id+"F2.opPattern","COPY",BODY,{"derivedFrom":makeQuery(id+"F1.opRevolve","SWEPT_BODY",BODY,{"disambiguationData":[OSD([sQuery(id+"F0.wireOp",EDGE,"E1")])]}),"instanceName":"1"}),"instanceName":"1"}),"instanceName":"1"}),"instanceName":"1"}),"instanceName":"1"});
            var Q260;
            Q260=makeQuery(id+"F10.opPattern","COPY",BODY,{"derivedFrom":makeQuery(id+"F8.opPattern","COPY",BODY,{"derivedFrom":makeQuery(id+"F6.opPattern","COPY",BODY,{"derivedFrom":makeQuery(id+"F5.opPattern","COPY",BODY,{"derivedFrom":makeQuery(id+"F3.opPattern","COPY",BODY,{"derivedFrom":makeQuery(id+"F2.opPattern","COPY",BODY,{"derivedFrom":makeQuery(id+"F1.opRevolve","SWEPT_BODY",BODY,{"disambiguationData":[OSD([sQuery(id+"F0.wireOp",EDGE,"E1")])]}),"instanceName":"1"}),"instanceName":"1"}),"instanceName":"1"}),"instanceName":"1"}),"instanceName":"1"}),"instanceName":"1"});
            var Q261;
            Q261=makeQuery(id+"F10.opPattern","COPY",BODY,{"derivedFrom":makeQuery(id+"F8.opPattern","COPY",BODY,{"derivedFrom":makeQuery(id+"F6.opPattern","COPY",BODY,{"derivedFrom":makeQuery(id+"F5.opPattern","COPY",BODY,{"derivedFrom":makeQuery(id+"F4.opPattern","COPY",BODY,{"derivedFrom":makeQuery(id+"F1.opRevolve","SWEPT_BODY",BODY,{"disambiguationData":[OSD([sQuery(id+"F0.wireOp",EDGE,"E1")])]}),"instanceName":"1"}),"instanceName":"1"}),"instanceName":"1"}),"instanceName":"1"}),"instanceName":"1"});
            var Q262;
            Q262=makeQuery(id+"F10.opPattern","COPY",BODY,{"derivedFrom":makeQuery(id+"F8.opPattern","COPY",BODY,{"derivedFrom":makeQuery(id+"F6.opPattern","COPY",BODY,{"derivedFrom":makeQuery(id+"F5.opPattern","COPY",BODY,{"derivedFrom":makeQuery(id+"F4.opPattern","COPY",BODY,{"derivedFrom":makeQuery(id+"F2.opPattern","COPY",BODY,{"derivedFrom":makeQuery(id+"F1.opRevolve","SWEPT_BODY",BODY,{"disambiguationData":[OSD([sQuery(id+"F0.wireOp",EDGE,"E1")])]}),"instanceName":"1"}),"instanceName":"1"}),"instanceName":"1"}),"instanceName":"1"}),"instanceName":"1"}),"instanceName":"1"});
            var Q263;
            Q263=makeQuery(id+"F10.opPattern","COPY",BODY,{"derivedFrom":makeQuery(id+"F8.opPattern","COPY",BODY,{"derivedFrom":makeQuery(id+"F6.opPattern","COPY",BODY,{"derivedFrom":makeQuery(id+"F5.opPattern","COPY",BODY,{"derivedFrom":makeQuery(id+"F4.opPattern","COPY",BODY,{"derivedFrom":makeQuery(id+"F3.opPattern","COPY",BODY,{"derivedFrom":makeQuery(id+"F2.opPattern","COPY",BODY,{"derivedFrom":makeQuery(id+"F1.opRevolve","SWEPT_BODY",BODY,{"disambiguationData":[OSD([sQuery(id+"F0.wireOp",EDGE,"E1")])]}),"instanceName":"1"}),"instanceName":"1"}),"instanceName":"1"}),"instanceName":"1"}),"instanceName":"1"}),"instanceName":"1"}),"instanceName":"1"});
            var Q264;
            Q264=makeQuery(id+"F10.opPattern","COPY",BODY,{"derivedFrom":makeQuery(id+"F8.opPattern","COPY",BODY,{"derivedFrom":makeQuery(id+"F7.opPattern","COPY",BODY,{"derivedFrom":makeQuery(id+"F1.opRevolve","SWEPT_BODY",BODY,{"disambiguationData":[OSD([sQuery(id+"F0.wireOp",EDGE,"E1")])]}),"instanceName":"1"}),"instanceName":"1"}),"instanceName":"1"});
            var Q265;
            Q265=makeQuery(id+"F10.opPattern","COPY",BODY,{"derivedFrom":makeQuery(id+"F8.opPattern","COPY",BODY,{"derivedFrom":makeQuery(id+"F7.opPattern","COPY",BODY,{"derivedFrom":makeQuery(id+"F2.opPattern","COPY",BODY,{"derivedFrom":makeQuery(id+"F1.opRevolve","SWEPT_BODY",BODY,{"disambiguationData":[OSD([sQuery(id+"F0.wireOp",EDGE,"E1")])]}),"instanceName":"1"}),"instanceName":"1"}),"instanceName":"1"}),"instanceName":"1"});
            var Q266;
            Q266=makeQuery(id+"F10.opPattern","COPY",BODY,{"derivedFrom":makeQuery(id+"F8.opPattern","COPY",BODY,{"derivedFrom":makeQuery(id+"F7.opPattern","COPY",BODY,{"derivedFrom":makeQuery(id+"F3.opPattern","COPY",BODY,{"derivedFrom":makeQuery(id+"F2.opPattern","COPY",BODY,{"derivedFrom":makeQuery(id+"F1.opRevolve","SWEPT_BODY",BODY,{"disambiguationData":[OSD([sQuery(id+"F0.wireOp",EDGE,"E1")])]}),"instanceName":"1"}),"instanceName":"1"}),"instanceName":"1"}),"instanceName":"1"}),"instanceName":"1"});
            var Q267;
            Q267=makeQuery(id+"F10.opPattern","COPY",BODY,{"derivedFrom":makeQuery(id+"F8.opPattern","COPY",BODY,{"derivedFrom":makeQuery(id+"F7.opPattern","COPY",BODY,{"derivedFrom":makeQuery(id+"F4.opPattern","COPY",BODY,{"derivedFrom":makeQuery(id+"F1.opRevolve","SWEPT_BODY",BODY,{"disambiguationData":[OSD([sQuery(id+"F0.wireOp",EDGE,"E1")])]}),"instanceName":"1"}),"instanceName":"1"}),"instanceName":"1"}),"instanceName":"1"});
            var Q268;
            Q268=makeQuery(id+"F10.opPattern","COPY",BODY,{"derivedFrom":makeQuery(id+"F8.opPattern","COPY",BODY,{"derivedFrom":makeQuery(id+"F7.opPattern","COPY",BODY,{"derivedFrom":makeQuery(id+"F4.opPattern","COPY",BODY,{"derivedFrom":makeQuery(id+"F2.opPattern","COPY",BODY,{"derivedFrom":makeQuery(id+"F1.opRevolve","SWEPT_BODY",BODY,{"disambiguationData":[OSD([sQuery(id+"F0.wireOp",EDGE,"E1")])]}),"instanceName":"1"}),"instanceName":"1"}),"instanceName":"1"}),"instanceName":"1"}),"instanceName":"1"});
            var Q269;
            Q269=makeQuery(id+"F10.opPattern","COPY",BODY,{"derivedFrom":makeQuery(id+"F8.opPattern","COPY",BODY,{"derivedFrom":makeQuery(id+"F7.opPattern","COPY",BODY,{"derivedFrom":makeQuery(id+"F4.opPattern","COPY",BODY,{"derivedFrom":makeQuery(id+"F3.opPattern","COPY",BODY,{"derivedFrom":makeQuery(id+"F2.opPattern","COPY",BODY,{"derivedFrom":makeQuery(id+"F1.opRevolve","SWEPT_BODY",BODY,{"disambiguationData":[OSD([sQuery(id+"F0.wireOp",EDGE,"E1")])]}),"instanceName":"1"}),"instanceName":"1"}),"instanceName":"1"}),"instanceName":"1"}),"instanceName":"1"}),"instanceName":"1"});
            var Q270;
            Q270=makeQuery(id+"F10.opPattern","COPY",BODY,{"derivedFrom":makeQuery(id+"F8.opPattern","COPY",BODY,{"derivedFrom":makeQuery(id+"F7.opPattern","COPY",BODY,{"derivedFrom":makeQuery(id+"F5.opPattern","COPY",BODY,{"derivedFrom":makeQuery(id+"F1.opRevolve","SWEPT_BODY",BODY,{"disambiguationData":[OSD([sQuery(id+"F0.wireOp",EDGE,"E1")])]}),"instanceName":"1"}),"instanceName":"1"}),"instanceName":"1"}),"instanceName":"1"});
            var Q271;
            Q271=makeQuery(id+"F10.opPattern","COPY",BODY,{"derivedFrom":makeQuery(id+"F8.opPattern","COPY",BODY,{"derivedFrom":makeQuery(id+"F7.opPattern","COPY",BODY,{"derivedFrom":makeQuery(id+"F5.opPattern","COPY",BODY,{"derivedFrom":makeQuery(id+"F2.opPattern","COPY",BODY,{"derivedFrom":makeQuery(id+"F1.opRevolve","SWEPT_BODY",BODY,{"disambiguationData":[OSD([sQuery(id+"F0.wireOp",EDGE,"E1")])]}),"instanceName":"1"}),"instanceName":"1"}),"instanceName":"1"}),"instanceName":"1"}),"instanceName":"1"});
            var Q272;
            Q272=makeQuery(id+"F10.opPattern","COPY",BODY,{"derivedFrom":makeQuery(id+"F8.opPattern","COPY",BODY,{"derivedFrom":makeQuery(id+"F7.opPattern","COPY",BODY,{"derivedFrom":makeQuery(id+"F5.opPattern","COPY",BODY,{"derivedFrom":makeQuery(id+"F3.opPattern","COPY",BODY,{"derivedFrom":makeQuery(id+"F2.opPattern","COPY",BODY,{"derivedFrom":makeQuery(id+"F1.opRevolve","SWEPT_BODY",BODY,{"disambiguationData":[OSD([sQuery(id+"F0.wireOp",EDGE,"E1")])]}),"instanceName":"1"}),"instanceName":"1"}),"instanceName":"1"}),"instanceName":"1"}),"instanceName":"1"}),"instanceName":"1"});
            var Q273;
            Q273=makeQuery(id+"F10.opPattern","COPY",BODY,{"derivedFrom":makeQuery(id+"F8.opPattern","COPY",BODY,{"derivedFrom":makeQuery(id+"F7.opPattern","COPY",BODY,{"derivedFrom":makeQuery(id+"F5.opPattern","COPY",BODY,{"derivedFrom":makeQuery(id+"F4.opPattern","COPY",BODY,{"derivedFrom":makeQuery(id+"F1.opRevolve","SWEPT_BODY",BODY,{"disambiguationData":[OSD([sQuery(id+"F0.wireOp",EDGE,"E1")])]}),"instanceName":"1"}),"instanceName":"1"}),"instanceName":"1"}),"instanceName":"1"}),"instanceName":"1"});
            var Q274;
            Q274=makeQuery(id+"F10.opPattern","COPY",BODY,{"derivedFrom":makeQuery(id+"F8.opPattern","COPY",BODY,{"derivedFrom":makeQuery(id+"F7.opPattern","COPY",BODY,{"derivedFrom":makeQuery(id+"F5.opPattern","COPY",BODY,{"derivedFrom":makeQuery(id+"F4.opPattern","COPY",BODY,{"derivedFrom":makeQuery(id+"F2.opPattern","COPY",BODY,{"derivedFrom":makeQuery(id+"F1.opRevolve","SWEPT_BODY",BODY,{"disambiguationData":[OSD([sQuery(id+"F0.wireOp",EDGE,"E1")])]}),"instanceName":"1"}),"instanceName":"1"}),"instanceName":"1"}),"instanceName":"1"}),"instanceName":"1"}),"instanceName":"1"});
            var Q275;
            Q275=makeQuery(id+"F10.opPattern","COPY",BODY,{"derivedFrom":makeQuery(id+"F8.opPattern","COPY",BODY,{"derivedFrom":makeQuery(id+"F7.opPattern","COPY",BODY,{"derivedFrom":makeQuery(id+"F5.opPattern","COPY",BODY,{"derivedFrom":makeQuery(id+"F4.opPattern","COPY",BODY,{"derivedFrom":makeQuery(id+"F3.opPattern","COPY",BODY,{"derivedFrom":makeQuery(id+"F2.opPattern","COPY",BODY,{"derivedFrom":makeQuery(id+"F1.opRevolve","SWEPT_BODY",BODY,{"disambiguationData":[OSD([sQuery(id+"F0.wireOp",EDGE,"E1")])]}),"instanceName":"1"}),"instanceName":"1"}),"instanceName":"1"}),"instanceName":"1"}),"instanceName":"1"}),"instanceName":"1"}),"instanceName":"1"});
            var Q276;
            Q276=makeQuery(id+"F10.opPattern","COPY",BODY,{"derivedFrom":makeQuery(id+"F8.opPattern","COPY",BODY,{"derivedFrom":makeQuery(id+"F7.opPattern","COPY",BODY,{"derivedFrom":makeQuery(id+"F6.opPattern","COPY",BODY,{"derivedFrom":makeQuery(id+"F1.opRevolve","SWEPT_BODY",BODY,{"disambiguationData":[OSD([sQuery(id+"F0.wireOp",EDGE,"E1")])]}),"instanceName":"1"}),"instanceName":"1"}),"instanceName":"1"}),"instanceName":"1"});
            var Q277;
            Q277=makeQuery(id+"F10.opPattern","COPY",BODY,{"derivedFrom":makeQuery(id+"F8.opPattern","COPY",BODY,{"derivedFrom":makeQuery(id+"F7.opPattern","COPY",BODY,{"derivedFrom":makeQuery(id+"F6.opPattern","COPY",BODY,{"derivedFrom":makeQuery(id+"F2.opPattern","COPY",BODY,{"derivedFrom":makeQuery(id+"F1.opRevolve","SWEPT_BODY",BODY,{"disambiguationData":[OSD([sQuery(id+"F0.wireOp",EDGE,"E1")])]}),"instanceName":"1"}),"instanceName":"1"}),"instanceName":"1"}),"instanceName":"1"}),"instanceName":"1"});
            var Q278;
            Q278=makeQuery(id+"F10.opPattern","COPY",BODY,{"derivedFrom":makeQuery(id+"F8.opPattern","COPY",BODY,{"derivedFrom":makeQuery(id+"F7.opPattern","COPY",BODY,{"derivedFrom":makeQuery(id+"F6.opPattern","COPY",BODY,{"derivedFrom":makeQuery(id+"F3.opPattern","COPY",BODY,{"derivedFrom":makeQuery(id+"F2.opPattern","COPY",BODY,{"derivedFrom":makeQuery(id+"F1.opRevolve","SWEPT_BODY",BODY,{"disambiguationData":[OSD([sQuery(id+"F0.wireOp",EDGE,"E1")])]}),"instanceName":"1"}),"instanceName":"1"}),"instanceName":"1"}),"instanceName":"1"}),"instanceName":"1"}),"instanceName":"1"});
            var Q279;
            Q279=makeQuery(id+"F10.opPattern","COPY",BODY,{"derivedFrom":makeQuery(id+"F8.opPattern","COPY",BODY,{"derivedFrom":makeQuery(id+"F7.opPattern","COPY",BODY,{"derivedFrom":makeQuery(id+"F6.opPattern","COPY",BODY,{"derivedFrom":makeQuery(id+"F4.opPattern","COPY",BODY,{"derivedFrom":makeQuery(id+"F1.opRevolve","SWEPT_BODY",BODY,{"disambiguationData":[OSD([sQuery(id+"F0.wireOp",EDGE,"E1")])]}),"instanceName":"1"}),"instanceName":"1"}),"instanceName":"1"}),"instanceName":"1"}),"instanceName":"1"});
            var Q280;
            Q280=makeQuery(id+"F10.opPattern","COPY",BODY,{"derivedFrom":makeQuery(id+"F8.opPattern","COPY",BODY,{"derivedFrom":makeQuery(id+"F7.opPattern","COPY",BODY,{"derivedFrom":makeQuery(id+"F6.opPattern","COPY",BODY,{"derivedFrom":makeQuery(id+"F4.opPattern","COPY",BODY,{"derivedFrom":makeQuery(id+"F2.opPattern","COPY",BODY,{"derivedFrom":makeQuery(id+"F1.opRevolve","SWEPT_BODY",BODY,{"disambiguationData":[OSD([sQuery(id+"F0.wireOp",EDGE,"E1")])]}),"instanceName":"1"}),"instanceName":"1"}),"instanceName":"1"}),"instanceName":"1"}),"instanceName":"1"}),"instanceName":"1"});
            var Q281;
            Q281=makeQuery(id+"F10.opPattern","COPY",BODY,{"derivedFrom":makeQuery(id+"F8.opPattern","COPY",BODY,{"derivedFrom":makeQuery(id+"F7.opPattern","COPY",BODY,{"derivedFrom":makeQuery(id+"F6.opPattern","COPY",BODY,{"derivedFrom":makeQuery(id+"F4.opPattern","COPY",BODY,{"derivedFrom":makeQuery(id+"F3.opPattern","COPY",BODY,{"derivedFrom":makeQuery(id+"F2.opPattern","COPY",BODY,{"derivedFrom":makeQuery(id+"F1.opRevolve","SWEPT_BODY",BODY,{"disambiguationData":[OSD([sQuery(id+"F0.wireOp",EDGE,"E1")])]}),"instanceName":"1"}),"instanceName":"1"}),"instanceName":"1"}),"instanceName":"1"}),"instanceName":"1"}),"instanceName":"1"}),"instanceName":"1"});
            var Q282;
            Q282=makeQuery(id+"F10.opPattern","COPY",BODY,{"derivedFrom":makeQuery(id+"F8.opPattern","COPY",BODY,{"derivedFrom":makeQuery(id+"F7.opPattern","COPY",BODY,{"derivedFrom":makeQuery(id+"F6.opPattern","COPY",BODY,{"derivedFrom":makeQuery(id+"F5.opPattern","COPY",BODY,{"derivedFrom":makeQuery(id+"F1.opRevolve","SWEPT_BODY",BODY,{"disambiguationData":[OSD([sQuery(id+"F0.wireOp",EDGE,"E1")])]}),"instanceName":"1"}),"instanceName":"1"}),"instanceName":"1"}),"instanceName":"1"}),"instanceName":"1"});
            var Q283;
            Q283=makeQuery(id+"F10.opPattern","COPY",BODY,{"derivedFrom":makeQuery(id+"F8.opPattern","COPY",BODY,{"derivedFrom":makeQuery(id+"F7.opPattern","COPY",BODY,{"derivedFrom":makeQuery(id+"F6.opPattern","COPY",BODY,{"derivedFrom":makeQuery(id+"F5.opPattern","COPY",BODY,{"derivedFrom":makeQuery(id+"F2.opPattern","COPY",BODY,{"derivedFrom":makeQuery(id+"F1.opRevolve","SWEPT_BODY",BODY,{"disambiguationData":[OSD([sQuery(id+"F0.wireOp",EDGE,"E1")])]}),"instanceName":"1"}),"instanceName":"1"}),"instanceName":"1"}),"instanceName":"1"}),"instanceName":"1"}),"instanceName":"1"});
            var Q284;
            Q284=makeQuery(id+"F10.opPattern","COPY",BODY,{"derivedFrom":makeQuery(id+"F8.opPattern","COPY",BODY,{"derivedFrom":makeQuery(id+"F7.opPattern","COPY",BODY,{"derivedFrom":makeQuery(id+"F6.opPattern","COPY",BODY,{"derivedFrom":makeQuery(id+"F5.opPattern","COPY",BODY,{"derivedFrom":makeQuery(id+"F3.opPattern","COPY",BODY,{"derivedFrom":makeQuery(id+"F2.opPattern","COPY",BODY,{"derivedFrom":makeQuery(id+"F1.opRevolve","SWEPT_BODY",BODY,{"disambiguationData":[OSD([sQuery(id+"F0.wireOp",EDGE,"E1")])]}),"instanceName":"1"}),"instanceName":"1"}),"instanceName":"1"}),"instanceName":"1"}),"instanceName":"1"}),"instanceName":"1"}),"instanceName":"1"});
            var Q285;
            Q285=makeQuery(id+"F10.opPattern","COPY",BODY,{"derivedFrom":makeQuery(id+"F8.opPattern","COPY",BODY,{"derivedFrom":makeQuery(id+"F7.opPattern","COPY",BODY,{"derivedFrom":makeQuery(id+"F6.opPattern","COPY",BODY,{"derivedFrom":makeQuery(id+"F5.opPattern","COPY",BODY,{"derivedFrom":makeQuery(id+"F4.opPattern","COPY",BODY,{"derivedFrom":makeQuery(id+"F1.opRevolve","SWEPT_BODY",BODY,{"disambiguationData":[OSD([sQuery(id+"F0.wireOp",EDGE,"E1")])]}),"instanceName":"1"}),"instanceName":"1"}),"instanceName":"1"}),"instanceName":"1"}),"instanceName":"1"}),"instanceName":"1"});
            var Q286;
            Q286=makeQuery(id+"F10.opPattern","COPY",BODY,{"derivedFrom":makeQuery(id+"F8.opPattern","COPY",BODY,{"derivedFrom":makeQuery(id+"F7.opPattern","COPY",BODY,{"derivedFrom":makeQuery(id+"F6.opPattern","COPY",BODY,{"derivedFrom":makeQuery(id+"F5.opPattern","COPY",BODY,{"derivedFrom":makeQuery(id+"F4.opPattern","COPY",BODY,{"derivedFrom":makeQuery(id+"F2.opPattern","COPY",BODY,{"derivedFrom":makeQuery(id+"F1.opRevolve","SWEPT_BODY",BODY,{"disambiguationData":[OSD([sQuery(id+"F0.wireOp",EDGE,"E1")])]}),"instanceName":"1"}),"instanceName":"1"}),"instanceName":"1"}),"instanceName":"1"}),"instanceName":"1"}),"instanceName":"1"}),"instanceName":"1"});
            var Q287;
            Q287=makeQuery(id+"F10.opPattern","COPY",BODY,{"derivedFrom":makeQuery(id+"F8.opPattern","COPY",BODY,{"derivedFrom":makeQuery(id+"F7.opPattern","COPY",BODY,{"derivedFrom":makeQuery(id+"F6.opPattern","COPY",BODY,{"derivedFrom":makeQuery(id+"F5.opPattern","COPY",BODY,{"derivedFrom":makeQuery(id+"F4.opPattern","COPY",BODY,{"derivedFrom":makeQuery(id+"F3.opPattern","COPY",BODY,{"derivedFrom":makeQuery(id+"F2.opPattern","COPY",BODY,{"derivedFrom":makeQuery(id+"F1.opRevolve","SWEPT_BODY",BODY,{"disambiguationData":[OSD([sQuery(id+"F0.wireOp",EDGE,"E1")])]}),"instanceName":"1"}),"instanceName":"1"}),"instanceName":"1"}),"instanceName":"1"}),"instanceName":"1"}),"instanceName":"1"}),"instanceName":"1"}),"instanceName":"1"});
            var Q288;
            Q288=makeQuery(id+"F10.opPattern","COPY",BODY,{"derivedFrom":makeQuery(id+"F9.opPattern","COPY",BODY,{"derivedFrom":makeQuery(id+"F1.opRevolve","SWEPT_BODY",BODY,{"disambiguationData":[OSD([sQuery(id+"F0.wireOp",EDGE,"E1")])]}),"instanceName":"1"}),"instanceName":"1"});
            var Q289;
            Q289=makeQuery(id+"F10.opPattern","COPY",BODY,{"derivedFrom":makeQuery(id+"F9.opPattern","COPY",BODY,{"derivedFrom":makeQuery(id+"F2.opPattern","COPY",BODY,{"derivedFrom":makeQuery(id+"F1.opRevolve","SWEPT_BODY",BODY,{"disambiguationData":[OSD([sQuery(id+"F0.wireOp",EDGE,"E1")])]}),"instanceName":"1"}),"instanceName":"1"}),"instanceName":"1"});
            var Q290;
            Q290=makeQuery(id+"F10.opPattern","COPY",BODY,{"derivedFrom":makeQuery(id+"F9.opPattern","COPY",BODY,{"derivedFrom":makeQuery(id+"F3.opPattern","COPY",BODY,{"derivedFrom":makeQuery(id+"F2.opPattern","COPY",BODY,{"derivedFrom":makeQuery(id+"F1.opRevolve","SWEPT_BODY",BODY,{"disambiguationData":[OSD([sQuery(id+"F0.wireOp",EDGE,"E1")])]}),"instanceName":"1"}),"instanceName":"1"}),"instanceName":"1"}),"instanceName":"1"});
            var Q291;
            Q291=makeQuery(id+"F10.opPattern","COPY",BODY,{"derivedFrom":makeQuery(id+"F9.opPattern","COPY",BODY,{"derivedFrom":makeQuery(id+"F4.opPattern","COPY",BODY,{"derivedFrom":makeQuery(id+"F1.opRevolve","SWEPT_BODY",BODY,{"disambiguationData":[OSD([sQuery(id+"F0.wireOp",EDGE,"E1")])]}),"instanceName":"1"}),"instanceName":"1"}),"instanceName":"1"});
            var Q292;
            Q292=makeQuery(id+"F10.opPattern","COPY",BODY,{"derivedFrom":makeQuery(id+"F9.opPattern","COPY",BODY,{"derivedFrom":makeQuery(id+"F4.opPattern","COPY",BODY,{"derivedFrom":makeQuery(id+"F2.opPattern","COPY",BODY,{"derivedFrom":makeQuery(id+"F1.opRevolve","SWEPT_BODY",BODY,{"disambiguationData":[OSD([sQuery(id+"F0.wireOp",EDGE,"E1")])]}),"instanceName":"1"}),"instanceName":"1"}),"instanceName":"1"}),"instanceName":"1"});
            var Q293;
            Q293=makeQuery(id+"F10.opPattern","COPY",BODY,{"derivedFrom":makeQuery(id+"F9.opPattern","COPY",BODY,{"derivedFrom":makeQuery(id+"F4.opPattern","COPY",BODY,{"derivedFrom":makeQuery(id+"F3.opPattern","COPY",BODY,{"derivedFrom":makeQuery(id+"F2.opPattern","COPY",BODY,{"derivedFrom":makeQuery(id+"F1.opRevolve","SWEPT_BODY",BODY,{"disambiguationData":[OSD([sQuery(id+"F0.wireOp",EDGE,"E1")])]}),"instanceName":"1"}),"instanceName":"1"}),"instanceName":"1"}),"instanceName":"1"}),"instanceName":"1"});
            var Q294;
            Q294=makeQuery(id+"F10.opPattern","COPY",BODY,{"derivedFrom":makeQuery(id+"F9.opPattern","COPY",BODY,{"derivedFrom":makeQuery(id+"F5.opPattern","COPY",BODY,{"derivedFrom":makeQuery(id+"F1.opRevolve","SWEPT_BODY",BODY,{"disambiguationData":[OSD([sQuery(id+"F0.wireOp",EDGE,"E1")])]}),"instanceName":"1"}),"instanceName":"1"}),"instanceName":"1"});
            var Q295;
            Q295=makeQuery(id+"F10.opPattern","COPY",BODY,{"derivedFrom":makeQuery(id+"F9.opPattern","COPY",BODY,{"derivedFrom":makeQuery(id+"F5.opPattern","COPY",BODY,{"derivedFrom":makeQuery(id+"F2.opPattern","COPY",BODY,{"derivedFrom":makeQuery(id+"F1.opRevolve","SWEPT_BODY",BODY,{"disambiguationData":[OSD([sQuery(id+"F0.wireOp",EDGE,"E1")])]}),"instanceName":"1"}),"instanceName":"1"}),"instanceName":"1"}),"instanceName":"1"});
            var Q296;
            Q296=makeQuery(id+"F10.opPattern","COPY",BODY,{"derivedFrom":makeQuery(id+"F9.opPattern","COPY",BODY,{"derivedFrom":makeQuery(id+"F5.opPattern","COPY",BODY,{"derivedFrom":makeQuery(id+"F3.opPattern","COPY",BODY,{"derivedFrom":makeQuery(id+"F2.opPattern","COPY",BODY,{"derivedFrom":makeQuery(id+"F1.opRevolve","SWEPT_BODY",BODY,{"disambiguationData":[OSD([sQuery(id+"F0.wireOp",EDGE,"E1")])]}),"instanceName":"1"}),"instanceName":"1"}),"instanceName":"1"}),"instanceName":"1"}),"instanceName":"1"});
            var Q297;
            Q297=makeQuery(id+"F10.opPattern","COPY",BODY,{"derivedFrom":makeQuery(id+"F9.opPattern","COPY",BODY,{"derivedFrom":makeQuery(id+"F5.opPattern","COPY",BODY,{"derivedFrom":makeQuery(id+"F4.opPattern","COPY",BODY,{"derivedFrom":makeQuery(id+"F1.opRevolve","SWEPT_BODY",BODY,{"disambiguationData":[OSD([sQuery(id+"F0.wireOp",EDGE,"E1")])]}),"instanceName":"1"}),"instanceName":"1"}),"instanceName":"1"}),"instanceName":"1"});
            var Q298;
            Q298=makeQuery(id+"F10.opPattern","COPY",BODY,{"derivedFrom":makeQuery(id+"F9.opPattern","COPY",BODY,{"derivedFrom":makeQuery(id+"F5.opPattern","COPY",BODY,{"derivedFrom":makeQuery(id+"F4.opPattern","COPY",BODY,{"derivedFrom":makeQuery(id+"F2.opPattern","COPY",BODY,{"derivedFrom":makeQuery(id+"F1.opRevolve","SWEPT_BODY",BODY,{"disambiguationData":[OSD([sQuery(id+"F0.wireOp",EDGE,"E1")])]}),"instanceName":"1"}),"instanceName":"1"}),"instanceName":"1"}),"instanceName":"1"}),"instanceName":"1"});
            var Q299;
            Q299=makeQuery(id+"F10.opPattern","COPY",BODY,{"derivedFrom":makeQuery(id+"F9.opPattern","COPY",BODY,{"derivedFrom":makeQuery(id+"F5.opPattern","COPY",BODY,{"derivedFrom":makeQuery(id+"F4.opPattern","COPY",BODY,{"derivedFrom":makeQuery(id+"F3.opPattern","COPY",BODY,{"derivedFrom":makeQuery(id+"F2.opPattern","COPY",BODY,{"derivedFrom":makeQuery(id+"F1.opRevolve","SWEPT_BODY",BODY,{"disambiguationData":[OSD([sQuery(id+"F0.wireOp",EDGE,"E1")])]}),"instanceName":"1"}),"instanceName":"1"}),"instanceName":"1"}),"instanceName":"1"}),"instanceName":"1"}),"instanceName":"1"});
            var Q300;
            Q300=makeQuery(id+"F10.opPattern","COPY",BODY,{"derivedFrom":makeQuery(id+"F9.opPattern","COPY",BODY,{"derivedFrom":makeQuery(id+"F6.opPattern","COPY",BODY,{"derivedFrom":makeQuery(id+"F1.opRevolve","SWEPT_BODY",BODY,{"disambiguationData":[OSD([sQuery(id+"F0.wireOp",EDGE,"E1")])]}),"instanceName":"1"}),"instanceName":"1"}),"instanceName":"1"});
            var Q301;
            Q301=makeQuery(id+"F10.opPattern","COPY",BODY,{"derivedFrom":makeQuery(id+"F9.opPattern","COPY",BODY,{"derivedFrom":makeQuery(id+"F6.opPattern","COPY",BODY,{"derivedFrom":makeQuery(id+"F2.opPattern","COPY",BODY,{"derivedFrom":makeQuery(id+"F1.opRevolve","SWEPT_BODY",BODY,{"disambiguationData":[OSD([sQuery(id+"F0.wireOp",EDGE,"E1")])]}),"instanceName":"1"}),"instanceName":"1"}),"instanceName":"1"}),"instanceName":"1"});
            var Q302;
            Q302=makeQuery(id+"F10.opPattern","COPY",BODY,{"derivedFrom":makeQuery(id+"F9.opPattern","COPY",BODY,{"derivedFrom":makeQuery(id+"F6.opPattern","COPY",BODY,{"derivedFrom":makeQuery(id+"F3.opPattern","COPY",BODY,{"derivedFrom":makeQuery(id+"F2.opPattern","COPY",BODY,{"derivedFrom":makeQuery(id+"F1.opRevolve","SWEPT_BODY",BODY,{"disambiguationData":[OSD([sQuery(id+"F0.wireOp",EDGE,"E1")])]}),"instanceName":"1"}),"instanceName":"1"}),"instanceName":"1"}),"instanceName":"1"}),"instanceName":"1"});
            var Q303;
            Q303=makeQuery(id+"F10.opPattern","COPY",BODY,{"derivedFrom":makeQuery(id+"F9.opPattern","COPY",BODY,{"derivedFrom":makeQuery(id+"F6.opPattern","COPY",BODY,{"derivedFrom":makeQuery(id+"F4.opPattern","COPY",BODY,{"derivedFrom":makeQuery(id+"F1.opRevolve","SWEPT_BODY",BODY,{"disambiguationData":[OSD([sQuery(id+"F0.wireOp",EDGE,"E1")])]}),"instanceName":"1"}),"instanceName":"1"}),"instanceName":"1"}),"instanceName":"1"});
            var Q304;
            Q304=makeQuery(id+"F10.opPattern","COPY",BODY,{"derivedFrom":makeQuery(id+"F9.opPattern","COPY",BODY,{"derivedFrom":makeQuery(id+"F6.opPattern","COPY",BODY,{"derivedFrom":makeQuery(id+"F4.opPattern","COPY",BODY,{"derivedFrom":makeQuery(id+"F2.opPattern","COPY",BODY,{"derivedFrom":makeQuery(id+"F1.opRevolve","SWEPT_BODY",BODY,{"disambiguationData":[OSD([sQuery(id+"F0.wireOp",EDGE,"E1")])]}),"instanceName":"1"}),"instanceName":"1"}),"instanceName":"1"}),"instanceName":"1"}),"instanceName":"1"});
            var Q305;
            Q305=makeQuery(id+"F10.opPattern","COPY",BODY,{"derivedFrom":makeQuery(id+"F9.opPattern","COPY",BODY,{"derivedFrom":makeQuery(id+"F6.opPattern","COPY",BODY,{"derivedFrom":makeQuery(id+"F4.opPattern","COPY",BODY,{"derivedFrom":makeQuery(id+"F3.opPattern","COPY",BODY,{"derivedFrom":makeQuery(id+"F2.opPattern","COPY",BODY,{"derivedFrom":makeQuery(id+"F1.opRevolve","SWEPT_BODY",BODY,{"disambiguationData":[OSD([sQuery(id+"F0.wireOp",EDGE,"E1")])]}),"instanceName":"1"}),"instanceName":"1"}),"instanceName":"1"}),"instanceName":"1"}),"instanceName":"1"}),"instanceName":"1"});
            var Q306;
            Q306=makeQuery(id+"F10.opPattern","COPY",BODY,{"derivedFrom":makeQuery(id+"F9.opPattern","COPY",BODY,{"derivedFrom":makeQuery(id+"F6.opPattern","COPY",BODY,{"derivedFrom":makeQuery(id+"F5.opPattern","COPY",BODY,{"derivedFrom":makeQuery(id+"F1.opRevolve","SWEPT_BODY",BODY,{"disambiguationData":[OSD([sQuery(id+"F0.wireOp",EDGE,"E1")])]}),"instanceName":"1"}),"instanceName":"1"}),"instanceName":"1"}),"instanceName":"1"});
            var Q307;
            Q307=makeQuery(id+"F10.opPattern","COPY",BODY,{"derivedFrom":makeQuery(id+"F9.opPattern","COPY",BODY,{"derivedFrom":makeQuery(id+"F6.opPattern","COPY",BODY,{"derivedFrom":makeQuery(id+"F5.opPattern","COPY",BODY,{"derivedFrom":makeQuery(id+"F2.opPattern","COPY",BODY,{"derivedFrom":makeQuery(id+"F1.opRevolve","SWEPT_BODY",BODY,{"disambiguationData":[OSD([sQuery(id+"F0.wireOp",EDGE,"E1")])]}),"instanceName":"1"}),"instanceName":"1"}),"instanceName":"1"}),"instanceName":"1"}),"instanceName":"1"});
            var Q308;
            Q308=makeQuery(id+"F10.opPattern","COPY",BODY,{"derivedFrom":makeQuery(id+"F9.opPattern","COPY",BODY,{"derivedFrom":makeQuery(id+"F6.opPattern","COPY",BODY,{"derivedFrom":makeQuery(id+"F5.opPattern","COPY",BODY,{"derivedFrom":makeQuery(id+"F3.opPattern","COPY",BODY,{"derivedFrom":makeQuery(id+"F2.opPattern","COPY",BODY,{"derivedFrom":makeQuery(id+"F1.opRevolve","SWEPT_BODY",BODY,{"disambiguationData":[OSD([sQuery(id+"F0.wireOp",EDGE,"E1")])]}),"instanceName":"1"}),"instanceName":"1"}),"instanceName":"1"}),"instanceName":"1"}),"instanceName":"1"}),"instanceName":"1"});
            var Q309;
            Q309=makeQuery(id+"F10.opPattern","COPY",BODY,{"derivedFrom":makeQuery(id+"F9.opPattern","COPY",BODY,{"derivedFrom":makeQuery(id+"F6.opPattern","COPY",BODY,{"derivedFrom":makeQuery(id+"F5.opPattern","COPY",BODY,{"derivedFrom":makeQuery(id+"F4.opPattern","COPY",BODY,{"derivedFrom":makeQuery(id+"F1.opRevolve","SWEPT_BODY",BODY,{"disambiguationData":[OSD([sQuery(id+"F0.wireOp",EDGE,"E1")])]}),"instanceName":"1"}),"instanceName":"1"}),"instanceName":"1"}),"instanceName":"1"}),"instanceName":"1"});
            var Q310;
            Q310=makeQuery(id+"F10.opPattern","COPY",BODY,{"derivedFrom":makeQuery(id+"F9.opPattern","COPY",BODY,{"derivedFrom":makeQuery(id+"F6.opPattern","COPY",BODY,{"derivedFrom":makeQuery(id+"F5.opPattern","COPY",BODY,{"derivedFrom":makeQuery(id+"F4.opPattern","COPY",BODY,{"derivedFrom":makeQuery(id+"F2.opPattern","COPY",BODY,{"derivedFrom":makeQuery(id+"F1.opRevolve","SWEPT_BODY",BODY,{"disambiguationData":[OSD([sQuery(id+"F0.wireOp",EDGE,"E1")])]}),"instanceName":"1"}),"instanceName":"1"}),"instanceName":"1"}),"instanceName":"1"}),"instanceName":"1"}),"instanceName":"1"});
            var Q311;
            Q311=makeQuery(id+"F10.opPattern","COPY",BODY,{"derivedFrom":makeQuery(id+"F9.opPattern","COPY",BODY,{"derivedFrom":makeQuery(id+"F6.opPattern","COPY",BODY,{"derivedFrom":makeQuery(id+"F5.opPattern","COPY",BODY,{"derivedFrom":makeQuery(id+"F4.opPattern","COPY",BODY,{"derivedFrom":makeQuery(id+"F3.opPattern","COPY",BODY,{"derivedFrom":makeQuery(id+"F2.opPattern","COPY",BODY,{"derivedFrom":makeQuery(id+"F1.opRevolve","SWEPT_BODY",BODY,{"disambiguationData":[OSD([sQuery(id+"F0.wireOp",EDGE,"E1")])]}),"instanceName":"1"}),"instanceName":"1"}),"instanceName":"1"}),"instanceName":"1"}),"instanceName":"1"}),"instanceName":"1"}),"instanceName":"1"});
            var Q312;
            Q312=makeQuery(id+"F10.opPattern","COPY",BODY,{"derivedFrom":makeQuery(id+"F9.opPattern","COPY",BODY,{"derivedFrom":makeQuery(id+"F7.opPattern","COPY",BODY,{"derivedFrom":makeQuery(id+"F1.opRevolve","SWEPT_BODY",BODY,{"disambiguationData":[OSD([sQuery(id+"F0.wireOp",EDGE,"E1")])]}),"instanceName":"1"}),"instanceName":"1"}),"instanceName":"1"});
            var Q313;
            Q313=makeQuery(id+"F10.opPattern","COPY",BODY,{"derivedFrom":makeQuery(id+"F9.opPattern","COPY",BODY,{"derivedFrom":makeQuery(id+"F7.opPattern","COPY",BODY,{"derivedFrom":makeQuery(id+"F2.opPattern","COPY",BODY,{"derivedFrom":makeQuery(id+"F1.opRevolve","SWEPT_BODY",BODY,{"disambiguationData":[OSD([sQuery(id+"F0.wireOp",EDGE,"E1")])]}),"instanceName":"1"}),"instanceName":"1"}),"instanceName":"1"}),"instanceName":"1"});
            var Q314;
            Q314=makeQuery(id+"F10.opPattern","COPY",BODY,{"derivedFrom":makeQuery(id+"F9.opPattern","COPY",BODY,{"derivedFrom":makeQuery(id+"F7.opPattern","COPY",BODY,{"derivedFrom":makeQuery(id+"F3.opPattern","COPY",BODY,{"derivedFrom":makeQuery(id+"F2.opPattern","COPY",BODY,{"derivedFrom":makeQuery(id+"F1.opRevolve","SWEPT_BODY",BODY,{"disambiguationData":[OSD([sQuery(id+"F0.wireOp",EDGE,"E1")])]}),"instanceName":"1"}),"instanceName":"1"}),"instanceName":"1"}),"instanceName":"1"}),"instanceName":"1"});
            var Q315;
            Q315=makeQuery(id+"F10.opPattern","COPY",BODY,{"derivedFrom":makeQuery(id+"F9.opPattern","COPY",BODY,{"derivedFrom":makeQuery(id+"F7.opPattern","COPY",BODY,{"derivedFrom":makeQuery(id+"F4.opPattern","COPY",BODY,{"derivedFrom":makeQuery(id+"F1.opRevolve","SWEPT_BODY",BODY,{"disambiguationData":[OSD([sQuery(id+"F0.wireOp",EDGE,"E1")])]}),"instanceName":"1"}),"instanceName":"1"}),"instanceName":"1"}),"instanceName":"1"});
            var Q316;
            Q316=makeQuery(id+"F10.opPattern","COPY",BODY,{"derivedFrom":makeQuery(id+"F9.opPattern","COPY",BODY,{"derivedFrom":makeQuery(id+"F7.opPattern","COPY",BODY,{"derivedFrom":makeQuery(id+"F4.opPattern","COPY",BODY,{"derivedFrom":makeQuery(id+"F2.opPattern","COPY",BODY,{"derivedFrom":makeQuery(id+"F1.opRevolve","SWEPT_BODY",BODY,{"disambiguationData":[OSD([sQuery(id+"F0.wireOp",EDGE,"E1")])]}),"instanceName":"1"}),"instanceName":"1"}),"instanceName":"1"}),"instanceName":"1"}),"instanceName":"1"});
            var Q317;
            Q317=makeQuery(id+"F10.opPattern","COPY",BODY,{"derivedFrom":makeQuery(id+"F9.opPattern","COPY",BODY,{"derivedFrom":makeQuery(id+"F7.opPattern","COPY",BODY,{"derivedFrom":makeQuery(id+"F4.opPattern","COPY",BODY,{"derivedFrom":makeQuery(id+"F3.opPattern","COPY",BODY,{"derivedFrom":makeQuery(id+"F2.opPattern","COPY",BODY,{"derivedFrom":makeQuery(id+"F1.opRevolve","SWEPT_BODY",BODY,{"disambiguationData":[OSD([sQuery(id+"F0.wireOp",EDGE,"E1")])]}),"instanceName":"1"}),"instanceName":"1"}),"instanceName":"1"}),"instanceName":"1"}),"instanceName":"1"}),"instanceName":"1"});
            var Q318;
            Q318=makeQuery(id+"F10.opPattern","COPY",BODY,{"derivedFrom":makeQuery(id+"F9.opPattern","COPY",BODY,{"derivedFrom":makeQuery(id+"F7.opPattern","COPY",BODY,{"derivedFrom":makeQuery(id+"F5.opPattern","COPY",BODY,{"derivedFrom":makeQuery(id+"F1.opRevolve","SWEPT_BODY",BODY,{"disambiguationData":[OSD([sQuery(id+"F0.wireOp",EDGE,"E1")])]}),"instanceName":"1"}),"instanceName":"1"}),"instanceName":"1"}),"instanceName":"1"});
            var Q319;
            Q319=makeQuery(id+"F10.opPattern","COPY",BODY,{"derivedFrom":makeQuery(id+"F9.opPattern","COPY",BODY,{"derivedFrom":makeQuery(id+"F7.opPattern","COPY",BODY,{"derivedFrom":makeQuery(id+"F5.opPattern","COPY",BODY,{"derivedFrom":makeQuery(id+"F2.opPattern","COPY",BODY,{"derivedFrom":makeQuery(id+"F1.opRevolve","SWEPT_BODY",BODY,{"disambiguationData":[OSD([sQuery(id+"F0.wireOp",EDGE,"E1")])]}),"instanceName":"1"}),"instanceName":"1"}),"instanceName":"1"}),"instanceName":"1"}),"instanceName":"1"});
            var Q320;
            Q320=makeQuery(id+"F10.opPattern","COPY",BODY,{"derivedFrom":makeQuery(id+"F9.opPattern","COPY",BODY,{"derivedFrom":makeQuery(id+"F7.opPattern","COPY",BODY,{"derivedFrom":makeQuery(id+"F5.opPattern","COPY",BODY,{"derivedFrom":makeQuery(id+"F3.opPattern","COPY",BODY,{"derivedFrom":makeQuery(id+"F2.opPattern","COPY",BODY,{"derivedFrom":makeQuery(id+"F1.opRevolve","SWEPT_BODY",BODY,{"disambiguationData":[OSD([sQuery(id+"F0.wireOp",EDGE,"E1")])]}),"instanceName":"1"}),"instanceName":"1"}),"instanceName":"1"}),"instanceName":"1"}),"instanceName":"1"}),"instanceName":"1"});
            var Q321;
            Q321=makeQuery(id+"F10.opPattern","COPY",BODY,{"derivedFrom":makeQuery(id+"F9.opPattern","COPY",BODY,{"derivedFrom":makeQuery(id+"F7.opPattern","COPY",BODY,{"derivedFrom":makeQuery(id+"F5.opPattern","COPY",BODY,{"derivedFrom":makeQuery(id+"F4.opPattern","COPY",BODY,{"derivedFrom":makeQuery(id+"F1.opRevolve","SWEPT_BODY",BODY,{"disambiguationData":[OSD([sQuery(id+"F0.wireOp",EDGE,"E1")])]}),"instanceName":"1"}),"instanceName":"1"}),"instanceName":"1"}),"instanceName":"1"}),"instanceName":"1"});
            var Q322;
            Q322=makeQuery(id+"F10.opPattern","COPY",BODY,{"derivedFrom":makeQuery(id+"F9.opPattern","COPY",BODY,{"derivedFrom":makeQuery(id+"F7.opPattern","COPY",BODY,{"derivedFrom":makeQuery(id+"F5.opPattern","COPY",BODY,{"derivedFrom":makeQuery(id+"F4.opPattern","COPY",BODY,{"derivedFrom":makeQuery(id+"F2.opPattern","COPY",BODY,{"derivedFrom":makeQuery(id+"F1.opRevolve","SWEPT_BODY",BODY,{"disambiguationData":[OSD([sQuery(id+"F0.wireOp",EDGE,"E1")])]}),"instanceName":"1"}),"instanceName":"1"}),"instanceName":"1"}),"instanceName":"1"}),"instanceName":"1"}),"instanceName":"1"});
            var Q323;
            Q323=makeQuery(id+"F10.opPattern","COPY",BODY,{"derivedFrom":makeQuery(id+"F9.opPattern","COPY",BODY,{"derivedFrom":makeQuery(id+"F7.opPattern","COPY",BODY,{"derivedFrom":makeQuery(id+"F5.opPattern","COPY",BODY,{"derivedFrom":makeQuery(id+"F4.opPattern","COPY",BODY,{"derivedFrom":makeQuery(id+"F3.opPattern","COPY",BODY,{"derivedFrom":makeQuery(id+"F2.opPattern","COPY",BODY,{"derivedFrom":makeQuery(id+"F1.opRevolve","SWEPT_BODY",BODY,{"disambiguationData":[OSD([sQuery(id+"F0.wireOp",EDGE,"E1")])]}),"instanceName":"1"}),"instanceName":"1"}),"instanceName":"1"}),"instanceName":"1"}),"instanceName":"1"}),"instanceName":"1"}),"instanceName":"1"});
            var Q324;
            Q324=makeQuery(id+"F10.opPattern","COPY",BODY,{"derivedFrom":makeQuery(id+"F9.opPattern","COPY",BODY,{"derivedFrom":makeQuery(id+"F7.opPattern","COPY",BODY,{"derivedFrom":makeQuery(id+"F6.opPattern","COPY",BODY,{"derivedFrom":makeQuery(id+"F1.opRevolve","SWEPT_BODY",BODY,{"disambiguationData":[OSD([sQuery(id+"F0.wireOp",EDGE,"E1")])]}),"instanceName":"1"}),"instanceName":"1"}),"instanceName":"1"}),"instanceName":"1"});
            var Q325;
            Q325=makeQuery(id+"F10.opPattern","COPY",BODY,{"derivedFrom":makeQuery(id+"F9.opPattern","COPY",BODY,{"derivedFrom":makeQuery(id+"F7.opPattern","COPY",BODY,{"derivedFrom":makeQuery(id+"F6.opPattern","COPY",BODY,{"derivedFrom":makeQuery(id+"F2.opPattern","COPY",BODY,{"derivedFrom":makeQuery(id+"F1.opRevolve","SWEPT_BODY",BODY,{"disambiguationData":[OSD([sQuery(id+"F0.wireOp",EDGE,"E1")])]}),"instanceName":"1"}),"instanceName":"1"}),"instanceName":"1"}),"instanceName":"1"}),"instanceName":"1"});
            var Q326;
            Q326=makeQuery(id+"F10.opPattern","COPY",BODY,{"derivedFrom":makeQuery(id+"F9.opPattern","COPY",BODY,{"derivedFrom":makeQuery(id+"F7.opPattern","COPY",BODY,{"derivedFrom":makeQuery(id+"F6.opPattern","COPY",BODY,{"derivedFrom":makeQuery(id+"F3.opPattern","COPY",BODY,{"derivedFrom":makeQuery(id+"F2.opPattern","COPY",BODY,{"derivedFrom":makeQuery(id+"F1.opRevolve","SWEPT_BODY",BODY,{"disambiguationData":[OSD([sQuery(id+"F0.wireOp",EDGE,"E1")])]}),"instanceName":"1"}),"instanceName":"1"}),"instanceName":"1"}),"instanceName":"1"}),"instanceName":"1"}),"instanceName":"1"});
            var Q327;
            Q327=makeQuery(id+"F10.opPattern","COPY",BODY,{"derivedFrom":makeQuery(id+"F9.opPattern","COPY",BODY,{"derivedFrom":makeQuery(id+"F7.opPattern","COPY",BODY,{"derivedFrom":makeQuery(id+"F6.opPattern","COPY",BODY,{"derivedFrom":makeQuery(id+"F4.opPattern","COPY",BODY,{"derivedFrom":makeQuery(id+"F1.opRevolve","SWEPT_BODY",BODY,{"disambiguationData":[OSD([sQuery(id+"F0.wireOp",EDGE,"E1")])]}),"instanceName":"1"}),"instanceName":"1"}),"instanceName":"1"}),"instanceName":"1"}),"instanceName":"1"});
            var Q328;
            Q328=makeQuery(id+"F10.opPattern","COPY",BODY,{"derivedFrom":makeQuery(id+"F9.opPattern","COPY",BODY,{"derivedFrom":makeQuery(id+"F7.opPattern","COPY",BODY,{"derivedFrom":makeQuery(id+"F6.opPattern","COPY",BODY,{"derivedFrom":makeQuery(id+"F4.opPattern","COPY",BODY,{"derivedFrom":makeQuery(id+"F2.opPattern","COPY",BODY,{"derivedFrom":makeQuery(id+"F1.opRevolve","SWEPT_BODY",BODY,{"disambiguationData":[OSD([sQuery(id+"F0.wireOp",EDGE,"E1")])]}),"instanceName":"1"}),"instanceName":"1"}),"instanceName":"1"}),"instanceName":"1"}),"instanceName":"1"}),"instanceName":"1"});
            var Q329;
            Q329=makeQuery(id+"F10.opPattern","COPY",BODY,{"derivedFrom":makeQuery(id+"F9.opPattern","COPY",BODY,{"derivedFrom":makeQuery(id+"F7.opPattern","COPY",BODY,{"derivedFrom":makeQuery(id+"F6.opPattern","COPY",BODY,{"derivedFrom":makeQuery(id+"F4.opPattern","COPY",BODY,{"derivedFrom":makeQuery(id+"F3.opPattern","COPY",BODY,{"derivedFrom":makeQuery(id+"F2.opPattern","COPY",BODY,{"derivedFrom":makeQuery(id+"F1.opRevolve","SWEPT_BODY",BODY,{"disambiguationData":[OSD([sQuery(id+"F0.wireOp",EDGE,"E1")])]}),"instanceName":"1"}),"instanceName":"1"}),"instanceName":"1"}),"instanceName":"1"}),"instanceName":"1"}),"instanceName":"1"}),"instanceName":"1"});
            var Q330;
            Q330=makeQuery(id+"F10.opPattern","COPY",BODY,{"derivedFrom":makeQuery(id+"F9.opPattern","COPY",BODY,{"derivedFrom":makeQuery(id+"F7.opPattern","COPY",BODY,{"derivedFrom":makeQuery(id+"F6.opPattern","COPY",BODY,{"derivedFrom":makeQuery(id+"F5.opPattern","COPY",BODY,{"derivedFrom":makeQuery(id+"F1.opRevolve","SWEPT_BODY",BODY,{"disambiguationData":[OSD([sQuery(id+"F0.wireOp",EDGE,"E1")])]}),"instanceName":"1"}),"instanceName":"1"}),"instanceName":"1"}),"instanceName":"1"}),"instanceName":"1"});
            var Q331;
            Q331=makeQuery(id+"F10.opPattern","COPY",BODY,{"derivedFrom":makeQuery(id+"F9.opPattern","COPY",BODY,{"derivedFrom":makeQuery(id+"F7.opPattern","COPY",BODY,{"derivedFrom":makeQuery(id+"F6.opPattern","COPY",BODY,{"derivedFrom":makeQuery(id+"F5.opPattern","COPY",BODY,{"derivedFrom":makeQuery(id+"F2.opPattern","COPY",BODY,{"derivedFrom":makeQuery(id+"F1.opRevolve","SWEPT_BODY",BODY,{"disambiguationData":[OSD([sQuery(id+"F0.wireOp",EDGE,"E1")])]}),"instanceName":"1"}),"instanceName":"1"}),"instanceName":"1"}),"instanceName":"1"}),"instanceName":"1"}),"instanceName":"1"});
            var Q332;
            Q332=makeQuery(id+"F10.opPattern","COPY",BODY,{"derivedFrom":makeQuery(id+"F9.opPattern","COPY",BODY,{"derivedFrom":makeQuery(id+"F7.opPattern","COPY",BODY,{"derivedFrom":makeQuery(id+"F6.opPattern","COPY",BODY,{"derivedFrom":makeQuery(id+"F5.opPattern","COPY",BODY,{"derivedFrom":makeQuery(id+"F3.opPattern","COPY",BODY,{"derivedFrom":makeQuery(id+"F2.opPattern","COPY",BODY,{"derivedFrom":makeQuery(id+"F1.opRevolve","SWEPT_BODY",BODY,{"disambiguationData":[OSD([sQuery(id+"F0.wireOp",EDGE,"E1")])]}),"instanceName":"1"}),"instanceName":"1"}),"instanceName":"1"}),"instanceName":"1"}),"instanceName":"1"}),"instanceName":"1"}),"instanceName":"1"});
            var Q333;
            Q333=makeQuery(id+"F10.opPattern","COPY",BODY,{"derivedFrom":makeQuery(id+"F9.opPattern","COPY",BODY,{"derivedFrom":makeQuery(id+"F7.opPattern","COPY",BODY,{"derivedFrom":makeQuery(id+"F6.opPattern","COPY",BODY,{"derivedFrom":makeQuery(id+"F5.opPattern","COPY",BODY,{"derivedFrom":makeQuery(id+"F4.opPattern","COPY",BODY,{"derivedFrom":makeQuery(id+"F1.opRevolve","SWEPT_BODY",BODY,{"disambiguationData":[OSD([sQuery(id+"F0.wireOp",EDGE,"E1")])]}),"instanceName":"1"}),"instanceName":"1"}),"instanceName":"1"}),"instanceName":"1"}),"instanceName":"1"}),"instanceName":"1"});
            var Q334;
            Q334=makeQuery(id+"F10.opPattern","COPY",BODY,{"derivedFrom":makeQuery(id+"F9.opPattern","COPY",BODY,{"derivedFrom":makeQuery(id+"F7.opPattern","COPY",BODY,{"derivedFrom":makeQuery(id+"F6.opPattern","COPY",BODY,{"derivedFrom":makeQuery(id+"F5.opPattern","COPY",BODY,{"derivedFrom":makeQuery(id+"F4.opPattern","COPY",BODY,{"derivedFrom":makeQuery(id+"F2.opPattern","COPY",BODY,{"derivedFrom":makeQuery(id+"F1.opRevolve","SWEPT_BODY",BODY,{"disambiguationData":[OSD([sQuery(id+"F0.wireOp",EDGE,"E1")])]}),"instanceName":"1"}),"instanceName":"1"}),"instanceName":"1"}),"instanceName":"1"}),"instanceName":"1"}),"instanceName":"1"}),"instanceName":"1"});
            var Q335;
            Q335=makeQuery(id+"F10.opPattern","COPY",BODY,{"derivedFrom":makeQuery(id+"F9.opPattern","COPY",BODY,{"derivedFrom":makeQuery(id+"F7.opPattern","COPY",BODY,{"derivedFrom":makeQuery(id+"F6.opPattern","COPY",BODY,{"derivedFrom":makeQuery(id+"F5.opPattern","COPY",BODY,{"derivedFrom":makeQuery(id+"F4.opPattern","COPY",BODY,{"derivedFrom":makeQuery(id+"F3.opPattern","COPY",BODY,{"derivedFrom":makeQuery(id+"F2.opPattern","COPY",BODY,{"derivedFrom":makeQuery(id+"F1.opRevolve","SWEPT_BODY",BODY,{"disambiguationData":[OSD([sQuery(id+"F0.wireOp",EDGE,"E1")])]}),"instanceName":"1"}),"instanceName":"1"}),"instanceName":"1"}),"instanceName":"1"}),"instanceName":"1"}),"instanceName":"1"}),"instanceName":"1"}),"instanceName":"1"});
            var Q336;
            Q336=makeQuery(id+"F10.opPattern","COPY",BODY,{"derivedFrom":makeQuery(id+"F9.opPattern","COPY",BODY,{"derivedFrom":makeQuery(id+"F8.opPattern","COPY",BODY,{"derivedFrom":makeQuery(id+"F1.opRevolve","SWEPT_BODY",BODY,{"disambiguationData":[OSD([sQuery(id+"F0.wireOp",EDGE,"E1")])]}),"instanceName":"1"}),"instanceName":"1"}),"instanceName":"1"});
            var Q337;
            Q337=makeQuery(id+"F10.opPattern","COPY",BODY,{"derivedFrom":makeQuery(id+"F9.opPattern","COPY",BODY,{"derivedFrom":makeQuery(id+"F8.opPattern","COPY",BODY,{"derivedFrom":makeQuery(id+"F2.opPattern","COPY",BODY,{"derivedFrom":makeQuery(id+"F1.opRevolve","SWEPT_BODY",BODY,{"disambiguationData":[OSD([sQuery(id+"F0.wireOp",EDGE,"E1")])]}),"instanceName":"1"}),"instanceName":"1"}),"instanceName":"1"}),"instanceName":"1"});
            var Q338;
            Q338=makeQuery(id+"F10.opPattern","COPY",BODY,{"derivedFrom":makeQuery(id+"F9.opPattern","COPY",BODY,{"derivedFrom":makeQuery(id+"F8.opPattern","COPY",BODY,{"derivedFrom":makeQuery(id+"F3.opPattern","COPY",BODY,{"derivedFrom":makeQuery(id+"F2.opPattern","COPY",BODY,{"derivedFrom":makeQuery(id+"F1.opRevolve","SWEPT_BODY",BODY,{"disambiguationData":[OSD([sQuery(id+"F0.wireOp",EDGE,"E1")])]}),"instanceName":"1"}),"instanceName":"1"}),"instanceName":"1"}),"instanceName":"1"}),"instanceName":"1"});
            var Q339;
            Q339=makeQuery(id+"F10.opPattern","COPY",BODY,{"derivedFrom":makeQuery(id+"F9.opPattern","COPY",BODY,{"derivedFrom":makeQuery(id+"F8.opPattern","COPY",BODY,{"derivedFrom":makeQuery(id+"F4.opPattern","COPY",BODY,{"derivedFrom":makeQuery(id+"F1.opRevolve","SWEPT_BODY",BODY,{"disambiguationData":[OSD([sQuery(id+"F0.wireOp",EDGE,"E1")])]}),"instanceName":"1"}),"instanceName":"1"}),"instanceName":"1"}),"instanceName":"1"});
            var Q340;
            Q340=makeQuery(id+"F10.opPattern","COPY",BODY,{"derivedFrom":makeQuery(id+"F9.opPattern","COPY",BODY,{"derivedFrom":makeQuery(id+"F8.opPattern","COPY",BODY,{"derivedFrom":makeQuery(id+"F4.opPattern","COPY",BODY,{"derivedFrom":makeQuery(id+"F2.opPattern","COPY",BODY,{"derivedFrom":makeQuery(id+"F1.opRevolve","SWEPT_BODY",BODY,{"disambiguationData":[OSD([sQuery(id+"F0.wireOp",EDGE,"E1")])]}),"instanceName":"1"}),"instanceName":"1"}),"instanceName":"1"}),"instanceName":"1"}),"instanceName":"1"});
            var Q341;
            Q341=makeQuery(id+"F10.opPattern","COPY",BODY,{"derivedFrom":makeQuery(id+"F9.opPattern","COPY",BODY,{"derivedFrom":makeQuery(id+"F8.opPattern","COPY",BODY,{"derivedFrom":makeQuery(id+"F4.opPattern","COPY",BODY,{"derivedFrom":makeQuery(id+"F3.opPattern","COPY",BODY,{"derivedFrom":makeQuery(id+"F2.opPattern","COPY",BODY,{"derivedFrom":makeQuery(id+"F1.opRevolve","SWEPT_BODY",BODY,{"disambiguationData":[OSD([sQuery(id+"F0.wireOp",EDGE,"E1")])]}),"instanceName":"1"}),"instanceName":"1"}),"instanceName":"1"}),"instanceName":"1"}),"instanceName":"1"}),"instanceName":"1"});
            var Q342;
            Q342=makeQuery(id+"F10.opPattern","COPY",BODY,{"derivedFrom":makeQuery(id+"F9.opPattern","COPY",BODY,{"derivedFrom":makeQuery(id+"F8.opPattern","COPY",BODY,{"derivedFrom":makeQuery(id+"F5.opPattern","COPY",BODY,{"derivedFrom":makeQuery(id+"F1.opRevolve","SWEPT_BODY",BODY,{"disambiguationData":[OSD([sQuery(id+"F0.wireOp",EDGE,"E1")])]}),"instanceName":"1"}),"instanceName":"1"}),"instanceName":"1"}),"instanceName":"1"});
            var Q343;
            Q343=makeQuery(id+"F10.opPattern","COPY",BODY,{"derivedFrom":makeQuery(id+"F9.opPattern","COPY",BODY,{"derivedFrom":makeQuery(id+"F8.opPattern","COPY",BODY,{"derivedFrom":makeQuery(id+"F5.opPattern","COPY",BODY,{"derivedFrom":makeQuery(id+"F2.opPattern","COPY",BODY,{"derivedFrom":makeQuery(id+"F1.opRevolve","SWEPT_BODY",BODY,{"disambiguationData":[OSD([sQuery(id+"F0.wireOp",EDGE,"E1")])]}),"instanceName":"1"}),"instanceName":"1"}),"instanceName":"1"}),"instanceName":"1"}),"instanceName":"1"});
            var Q344;
            Q344=makeQuery(id+"F10.opPattern","COPY",BODY,{"derivedFrom":makeQuery(id+"F9.opPattern","COPY",BODY,{"derivedFrom":makeQuery(id+"F8.opPattern","COPY",BODY,{"derivedFrom":makeQuery(id+"F5.opPattern","COPY",BODY,{"derivedFrom":makeQuery(id+"F3.opPattern","COPY",BODY,{"derivedFrom":makeQuery(id+"F2.opPattern","COPY",BODY,{"derivedFrom":makeQuery(id+"F1.opRevolve","SWEPT_BODY",BODY,{"disambiguationData":[OSD([sQuery(id+"F0.wireOp",EDGE,"E1")])]}),"instanceName":"1"}),"instanceName":"1"}),"instanceName":"1"}),"instanceName":"1"}),"instanceName":"1"}),"instanceName":"1"});
            var Q345;
            Q345=makeQuery(id+"F10.opPattern","COPY",BODY,{"derivedFrom":makeQuery(id+"F9.opPattern","COPY",BODY,{"derivedFrom":makeQuery(id+"F8.opPattern","COPY",BODY,{"derivedFrom":makeQuery(id+"F5.opPattern","COPY",BODY,{"derivedFrom":makeQuery(id+"F4.opPattern","COPY",BODY,{"derivedFrom":makeQuery(id+"F1.opRevolve","SWEPT_BODY",BODY,{"disambiguationData":[OSD([sQuery(id+"F0.wireOp",EDGE,"E1")])]}),"instanceName":"1"}),"instanceName":"1"}),"instanceName":"1"}),"instanceName":"1"}),"instanceName":"1"});
            var Q346;
            Q346=makeQuery(id+"F10.opPattern","COPY",BODY,{"derivedFrom":makeQuery(id+"F9.opPattern","COPY",BODY,{"derivedFrom":makeQuery(id+"F8.opPattern","COPY",BODY,{"derivedFrom":makeQuery(id+"F5.opPattern","COPY",BODY,{"derivedFrom":makeQuery(id+"F4.opPattern","COPY",BODY,{"derivedFrom":makeQuery(id+"F2.opPattern","COPY",BODY,{"derivedFrom":makeQuery(id+"F1.opRevolve","SWEPT_BODY",BODY,{"disambiguationData":[OSD([sQuery(id+"F0.wireOp",EDGE,"E1")])]}),"instanceName":"1"}),"instanceName":"1"}),"instanceName":"1"}),"instanceName":"1"}),"instanceName":"1"}),"instanceName":"1"});
            var Q347;
            Q347=makeQuery(id+"F10.opPattern","COPY",BODY,{"derivedFrom":makeQuery(id+"F9.opPattern","COPY",BODY,{"derivedFrom":makeQuery(id+"F8.opPattern","COPY",BODY,{"derivedFrom":makeQuery(id+"F5.opPattern","COPY",BODY,{"derivedFrom":makeQuery(id+"F4.opPattern","COPY",BODY,{"derivedFrom":makeQuery(id+"F3.opPattern","COPY",BODY,{"derivedFrom":makeQuery(id+"F2.opPattern","COPY",BODY,{"derivedFrom":makeQuery(id+"F1.opRevolve","SWEPT_BODY",BODY,{"disambiguationData":[OSD([sQuery(id+"F0.wireOp",EDGE,"E1")])]}),"instanceName":"1"}),"instanceName":"1"}),"instanceName":"1"}),"instanceName":"1"}),"instanceName":"1"}),"instanceName":"1"}),"instanceName":"1"});
            var Q348;
            Q348=makeQuery(id+"F10.opPattern","COPY",BODY,{"derivedFrom":makeQuery(id+"F9.opPattern","COPY",BODY,{"derivedFrom":makeQuery(id+"F8.opPattern","COPY",BODY,{"derivedFrom":makeQuery(id+"F6.opPattern","COPY",BODY,{"derivedFrom":makeQuery(id+"F1.opRevolve","SWEPT_BODY",BODY,{"disambiguationData":[OSD([sQuery(id+"F0.wireOp",EDGE,"E1")])]}),"instanceName":"1"}),"instanceName":"1"}),"instanceName":"1"}),"instanceName":"1"});
            var Q349;
            Q349=makeQuery(id+"F10.opPattern","COPY",BODY,{"derivedFrom":makeQuery(id+"F9.opPattern","COPY",BODY,{"derivedFrom":makeQuery(id+"F8.opPattern","COPY",BODY,{"derivedFrom":makeQuery(id+"F6.opPattern","COPY",BODY,{"derivedFrom":makeQuery(id+"F2.opPattern","COPY",BODY,{"derivedFrom":makeQuery(id+"F1.opRevolve","SWEPT_BODY",BODY,{"disambiguationData":[OSD([sQuery(id+"F0.wireOp",EDGE,"E1")])]}),"instanceName":"1"}),"instanceName":"1"}),"instanceName":"1"}),"instanceName":"1"}),"instanceName":"1"});
            var Q350;
            Q350=makeQuery(id+"F10.opPattern","COPY",BODY,{"derivedFrom":makeQuery(id+"F9.opPattern","COPY",BODY,{"derivedFrom":makeQuery(id+"F8.opPattern","COPY",BODY,{"derivedFrom":makeQuery(id+"F6.opPattern","COPY",BODY,{"derivedFrom":makeQuery(id+"F3.opPattern","COPY",BODY,{"derivedFrom":makeQuery(id+"F2.opPattern","COPY",BODY,{"derivedFrom":makeQuery(id+"F1.opRevolve","SWEPT_BODY",BODY,{"disambiguationData":[OSD([sQuery(id+"F0.wireOp",EDGE,"E1")])]}),"instanceName":"1"}),"instanceName":"1"}),"instanceName":"1"}),"instanceName":"1"}),"instanceName":"1"}),"instanceName":"1"});
            var Q351;
            Q351=makeQuery(id+"F10.opPattern","COPY",BODY,{"derivedFrom":makeQuery(id+"F9.opPattern","COPY",BODY,{"derivedFrom":makeQuery(id+"F8.opPattern","COPY",BODY,{"derivedFrom":makeQuery(id+"F6.opPattern","COPY",BODY,{"derivedFrom":makeQuery(id+"F4.opPattern","COPY",BODY,{"derivedFrom":makeQuery(id+"F1.opRevolve","SWEPT_BODY",BODY,{"disambiguationData":[OSD([sQuery(id+"F0.wireOp",EDGE,"E1")])]}),"instanceName":"1"}),"instanceName":"1"}),"instanceName":"1"}),"instanceName":"1"}),"instanceName":"1"});
            var Q352;
            Q352=makeQuery(id+"F10.opPattern","COPY",BODY,{"derivedFrom":makeQuery(id+"F9.opPattern","COPY",BODY,{"derivedFrom":makeQuery(id+"F8.opPattern","COPY",BODY,{"derivedFrom":makeQuery(id+"F6.opPattern","COPY",BODY,{"derivedFrom":makeQuery(id+"F4.opPattern","COPY",BODY,{"derivedFrom":makeQuery(id+"F2.opPattern","COPY",BODY,{"derivedFrom":makeQuery(id+"F1.opRevolve","SWEPT_BODY",BODY,{"disambiguationData":[OSD([sQuery(id+"F0.wireOp",EDGE,"E1")])]}),"instanceName":"1"}),"instanceName":"1"}),"instanceName":"1"}),"instanceName":"1"}),"instanceName":"1"}),"instanceName":"1"});
            var Q353;
            Q353=makeQuery(id+"F10.opPattern","COPY",BODY,{"derivedFrom":makeQuery(id+"F9.opPattern","COPY",BODY,{"derivedFrom":makeQuery(id+"F8.opPattern","COPY",BODY,{"derivedFrom":makeQuery(id+"F6.opPattern","COPY",BODY,{"derivedFrom":makeQuery(id+"F4.opPattern","COPY",BODY,{"derivedFrom":makeQuery(id+"F3.opPattern","COPY",BODY,{"derivedFrom":makeQuery(id+"F2.opPattern","COPY",BODY,{"derivedFrom":makeQuery(id+"F1.opRevolve","SWEPT_BODY",BODY,{"disambiguationData":[OSD([sQuery(id+"F0.wireOp",EDGE,"E1")])]}),"instanceName":"1"}),"instanceName":"1"}),"instanceName":"1"}),"instanceName":"1"}),"instanceName":"1"}),"instanceName":"1"}),"instanceName":"1"});
            var Q354;
            Q354=makeQuery(id+"F10.opPattern","COPY",BODY,{"derivedFrom":makeQuery(id+"F9.opPattern","COPY",BODY,{"derivedFrom":makeQuery(id+"F8.opPattern","COPY",BODY,{"derivedFrom":makeQuery(id+"F6.opPattern","COPY",BODY,{"derivedFrom":makeQuery(id+"F5.opPattern","COPY",BODY,{"derivedFrom":makeQuery(id+"F1.opRevolve","SWEPT_BODY",BODY,{"disambiguationData":[OSD([sQuery(id+"F0.wireOp",EDGE,"E1")])]}),"instanceName":"1"}),"instanceName":"1"}),"instanceName":"1"}),"instanceName":"1"}),"instanceName":"1"});
            var Q355;
            Q355=makeQuery(id+"F10.opPattern","COPY",BODY,{"derivedFrom":makeQuery(id+"F9.opPattern","COPY",BODY,{"derivedFrom":makeQuery(id+"F8.opPattern","COPY",BODY,{"derivedFrom":makeQuery(id+"F6.opPattern","COPY",BODY,{"derivedFrom":makeQuery(id+"F5.opPattern","COPY",BODY,{"derivedFrom":makeQuery(id+"F2.opPattern","COPY",BODY,{"derivedFrom":makeQuery(id+"F1.opRevolve","SWEPT_BODY",BODY,{"disambiguationData":[OSD([sQuery(id+"F0.wireOp",EDGE,"E1")])]}),"instanceName":"1"}),"instanceName":"1"}),"instanceName":"1"}),"instanceName":"1"}),"instanceName":"1"}),"instanceName":"1"});
            var Q356;
            Q356=makeQuery(id+"F10.opPattern","COPY",BODY,{"derivedFrom":makeQuery(id+"F9.opPattern","COPY",BODY,{"derivedFrom":makeQuery(id+"F8.opPattern","COPY",BODY,{"derivedFrom":makeQuery(id+"F6.opPattern","COPY",BODY,{"derivedFrom":makeQuery(id+"F5.opPattern","COPY",BODY,{"derivedFrom":makeQuery(id+"F3.opPattern","COPY",BODY,{"derivedFrom":makeQuery(id+"F2.opPattern","COPY",BODY,{"derivedFrom":makeQuery(id+"F1.opRevolve","SWEPT_BODY",BODY,{"disambiguationData":[OSD([sQuery(id+"F0.wireOp",EDGE,"E1")])]}),"instanceName":"1"}),"instanceName":"1"}),"instanceName":"1"}),"instanceName":"1"}),"instanceName":"1"}),"instanceName":"1"}),"instanceName":"1"});
            var Q357;
            Q357=makeQuery(id+"F10.opPattern","COPY",BODY,{"derivedFrom":makeQuery(id+"F9.opPattern","COPY",BODY,{"derivedFrom":makeQuery(id+"F8.opPattern","COPY",BODY,{"derivedFrom":makeQuery(id+"F6.opPattern","COPY",BODY,{"derivedFrom":makeQuery(id+"F5.opPattern","COPY",BODY,{"derivedFrom":makeQuery(id+"F4.opPattern","COPY",BODY,{"derivedFrom":makeQuery(id+"F1.opRevolve","SWEPT_BODY",BODY,{"disambiguationData":[OSD([sQuery(id+"F0.wireOp",EDGE,"E1")])]}),"instanceName":"1"}),"instanceName":"1"}),"instanceName":"1"}),"instanceName":"1"}),"instanceName":"1"}),"instanceName":"1"});
            var Q358;
            Q358=makeQuery(id+"F10.opPattern","COPY",BODY,{"derivedFrom":makeQuery(id+"F9.opPattern","COPY",BODY,{"derivedFrom":makeQuery(id+"F8.opPattern","COPY",BODY,{"derivedFrom":makeQuery(id+"F6.opPattern","COPY",BODY,{"derivedFrom":makeQuery(id+"F5.opPattern","COPY",BODY,{"derivedFrom":makeQuery(id+"F4.opPattern","COPY",BODY,{"derivedFrom":makeQuery(id+"F2.opPattern","COPY",BODY,{"derivedFrom":makeQuery(id+"F1.opRevolve","SWEPT_BODY",BODY,{"disambiguationData":[OSD([sQuery(id+"F0.wireOp",EDGE,"E1")])]}),"instanceName":"1"}),"instanceName":"1"}),"instanceName":"1"}),"instanceName":"1"}),"instanceName":"1"}),"instanceName":"1"}),"instanceName":"1"});
            var Q359;
            Q359=makeQuery(id+"F10.opPattern","COPY",BODY,{"derivedFrom":makeQuery(id+"F9.opPattern","COPY",BODY,{"derivedFrom":makeQuery(id+"F8.opPattern","COPY",BODY,{"derivedFrom":makeQuery(id+"F6.opPattern","COPY",BODY,{"derivedFrom":makeQuery(id+"F5.opPattern","COPY",BODY,{"derivedFrom":makeQuery(id+"F4.opPattern","COPY",BODY,{"derivedFrom":makeQuery(id+"F3.opPattern","COPY",BODY,{"derivedFrom":makeQuery(id+"F2.opPattern","COPY",BODY,{"derivedFrom":makeQuery(id+"F1.opRevolve","SWEPT_BODY",BODY,{"disambiguationData":[OSD([sQuery(id+"F0.wireOp",EDGE,"E1")])]}),"instanceName":"1"}),"instanceName":"1"}),"instanceName":"1"}),"instanceName":"1"}),"instanceName":"1"}),"instanceName":"1"}),"instanceName":"1"}),"instanceName":"1"});
            var Q360;
            Q360=makeQuery(id+"F10.opPattern","COPY",BODY,{"derivedFrom":makeQuery(id+"F9.opPattern","COPY",BODY,{"derivedFrom":makeQuery(id+"F8.opPattern","COPY",BODY,{"derivedFrom":makeQuery(id+"F7.opPattern","COPY",BODY,{"derivedFrom":makeQuery(id+"F1.opRevolve","SWEPT_BODY",BODY,{"disambiguationData":[OSD([sQuery(id+"F0.wireOp",EDGE,"E1")])]}),"instanceName":"1"}),"instanceName":"1"}),"instanceName":"1"}),"instanceName":"1"});
            var Q361;
            Q361=makeQuery(id+"F10.opPattern","COPY",BODY,{"derivedFrom":makeQuery(id+"F9.opPattern","COPY",BODY,{"derivedFrom":makeQuery(id+"F8.opPattern","COPY",BODY,{"derivedFrom":makeQuery(id+"F7.opPattern","COPY",BODY,{"derivedFrom":makeQuery(id+"F2.opPattern","COPY",BODY,{"derivedFrom":makeQuery(id+"F1.opRevolve","SWEPT_BODY",BODY,{"disambiguationData":[OSD([sQuery(id+"F0.wireOp",EDGE,"E1")])]}),"instanceName":"1"}),"instanceName":"1"}),"instanceName":"1"}),"instanceName":"1"}),"instanceName":"1"});
            var Q362;
            Q362=makeQuery(id+"F10.opPattern","COPY",BODY,{"derivedFrom":makeQuery(id+"F9.opPattern","COPY",BODY,{"derivedFrom":makeQuery(id+"F8.opPattern","COPY",BODY,{"derivedFrom":makeQuery(id+"F7.opPattern","COPY",BODY,{"derivedFrom":makeQuery(id+"F3.opPattern","COPY",BODY,{"derivedFrom":makeQuery(id+"F2.opPattern","COPY",BODY,{"derivedFrom":makeQuery(id+"F1.opRevolve","SWEPT_BODY",BODY,{"disambiguationData":[OSD([sQuery(id+"F0.wireOp",EDGE,"E1")])]}),"instanceName":"1"}),"instanceName":"1"}),"instanceName":"1"}),"instanceName":"1"}),"instanceName":"1"}),"instanceName":"1"});
            var Q363;
            Q363=makeQuery(id+"F10.opPattern","COPY",BODY,{"derivedFrom":makeQuery(id+"F9.opPattern","COPY",BODY,{"derivedFrom":makeQuery(id+"F8.opPattern","COPY",BODY,{"derivedFrom":makeQuery(id+"F7.opPattern","COPY",BODY,{"derivedFrom":makeQuery(id+"F4.opPattern","COPY",BODY,{"derivedFrom":makeQuery(id+"F1.opRevolve","SWEPT_BODY",BODY,{"disambiguationData":[OSD([sQuery(id+"F0.wireOp",EDGE,"E1")])]}),"instanceName":"1"}),"instanceName":"1"}),"instanceName":"1"}),"instanceName":"1"}),"instanceName":"1"});
            var Q364;
            Q364=makeQuery(id+"F10.opPattern","COPY",BODY,{"derivedFrom":makeQuery(id+"F9.opPattern","COPY",BODY,{"derivedFrom":makeQuery(id+"F8.opPattern","COPY",BODY,{"derivedFrom":makeQuery(id+"F7.opPattern","COPY",BODY,{"derivedFrom":makeQuery(id+"F4.opPattern","COPY",BODY,{"derivedFrom":makeQuery(id+"F2.opPattern","COPY",BODY,{"derivedFrom":makeQuery(id+"F1.opRevolve","SWEPT_BODY",BODY,{"disambiguationData":[OSD([sQuery(id+"F0.wireOp",EDGE,"E1")])]}),"instanceName":"1"}),"instanceName":"1"}),"instanceName":"1"}),"instanceName":"1"}),"instanceName":"1"}),"instanceName":"1"});
            var Q365;
            Q365=makeQuery(id+"F10.opPattern","COPY",BODY,{"derivedFrom":makeQuery(id+"F9.opPattern","COPY",BODY,{"derivedFrom":makeQuery(id+"F8.opPattern","COPY",BODY,{"derivedFrom":makeQuery(id+"F7.opPattern","COPY",BODY,{"derivedFrom":makeQuery(id+"F4.opPattern","COPY",BODY,{"derivedFrom":makeQuery(id+"F3.opPattern","COPY",BODY,{"derivedFrom":makeQuery(id+"F2.opPattern","COPY",BODY,{"derivedFrom":makeQuery(id+"F1.opRevolve","SWEPT_BODY",BODY,{"disambiguationData":[OSD([sQuery(id+"F0.wireOp",EDGE,"E1")])]}),"instanceName":"1"}),"instanceName":"1"}),"instanceName":"1"}),"instanceName":"1"}),"instanceName":"1"}),"instanceName":"1"}),"instanceName":"1"});
            var Q366;
            Q366=makeQuery(id+"F10.opPattern","COPY",BODY,{"derivedFrom":makeQuery(id+"F9.opPattern","COPY",BODY,{"derivedFrom":makeQuery(id+"F8.opPattern","COPY",BODY,{"derivedFrom":makeQuery(id+"F7.opPattern","COPY",BODY,{"derivedFrom":makeQuery(id+"F5.opPattern","COPY",BODY,{"derivedFrom":makeQuery(id+"F1.opRevolve","SWEPT_BODY",BODY,{"disambiguationData":[OSD([sQuery(id+"F0.wireOp",EDGE,"E1")])]}),"instanceName":"1"}),"instanceName":"1"}),"instanceName":"1"}),"instanceName":"1"}),"instanceName":"1"});
            var Q367;
            Q367=makeQuery(id+"F10.opPattern","COPY",BODY,{"derivedFrom":makeQuery(id+"F9.opPattern","COPY",BODY,{"derivedFrom":makeQuery(id+"F8.opPattern","COPY",BODY,{"derivedFrom":makeQuery(id+"F7.opPattern","COPY",BODY,{"derivedFrom":makeQuery(id+"F5.opPattern","COPY",BODY,{"derivedFrom":makeQuery(id+"F2.opPattern","COPY",BODY,{"derivedFrom":makeQuery(id+"F1.opRevolve","SWEPT_BODY",BODY,{"disambiguationData":[OSD([sQuery(id+"F0.wireOp",EDGE,"E1")])]}),"instanceName":"1"}),"instanceName":"1"}),"instanceName":"1"}),"instanceName":"1"}),"instanceName":"1"}),"instanceName":"1"});
            var Q368;
            Q368=makeQuery(id+"F10.opPattern","COPY",BODY,{"derivedFrom":makeQuery(id+"F9.opPattern","COPY",BODY,{"derivedFrom":makeQuery(id+"F8.opPattern","COPY",BODY,{"derivedFrom":makeQuery(id+"F7.opPattern","COPY",BODY,{"derivedFrom":makeQuery(id+"F5.opPattern","COPY",BODY,{"derivedFrom":makeQuery(id+"F3.opPattern","COPY",BODY,{"derivedFrom":makeQuery(id+"F2.opPattern","COPY",BODY,{"derivedFrom":makeQuery(id+"F1.opRevolve","SWEPT_BODY",BODY,{"disambiguationData":[OSD([sQuery(id+"F0.wireOp",EDGE,"E1")])]}),"instanceName":"1"}),"instanceName":"1"}),"instanceName":"1"}),"instanceName":"1"}),"instanceName":"1"}),"instanceName":"1"}),"instanceName":"1"});
            var Q369;
            Q369=makeQuery(id+"F10.opPattern","COPY",BODY,{"derivedFrom":makeQuery(id+"F9.opPattern","COPY",BODY,{"derivedFrom":makeQuery(id+"F8.opPattern","COPY",BODY,{"derivedFrom":makeQuery(id+"F7.opPattern","COPY",BODY,{"derivedFrom":makeQuery(id+"F5.opPattern","COPY",BODY,{"derivedFrom":makeQuery(id+"F4.opPattern","COPY",BODY,{"derivedFrom":makeQuery(id+"F1.opRevolve","SWEPT_BODY",BODY,{"disambiguationData":[OSD([sQuery(id+"F0.wireOp",EDGE,"E1")])]}),"instanceName":"1"}),"instanceName":"1"}),"instanceName":"1"}),"instanceName":"1"}),"instanceName":"1"}),"instanceName":"1"});
            var Q370;
            Q370=makeQuery(id+"F10.opPattern","COPY",BODY,{"derivedFrom":makeQuery(id+"F9.opPattern","COPY",BODY,{"derivedFrom":makeQuery(id+"F8.opPattern","COPY",BODY,{"derivedFrom":makeQuery(id+"F7.opPattern","COPY",BODY,{"derivedFrom":makeQuery(id+"F5.opPattern","COPY",BODY,{"derivedFrom":makeQuery(id+"F4.opPattern","COPY",BODY,{"derivedFrom":makeQuery(id+"F2.opPattern","COPY",BODY,{"derivedFrom":makeQuery(id+"F1.opRevolve","SWEPT_BODY",BODY,{"disambiguationData":[OSD([sQuery(id+"F0.wireOp",EDGE,"E1")])]}),"instanceName":"1"}),"instanceName":"1"}),"instanceName":"1"}),"instanceName":"1"}),"instanceName":"1"}),"instanceName":"1"}),"instanceName":"1"});
            var Q371;
            Q371=makeQuery(id+"F10.opPattern","COPY",BODY,{"derivedFrom":makeQuery(id+"F9.opPattern","COPY",BODY,{"derivedFrom":makeQuery(id+"F8.opPattern","COPY",BODY,{"derivedFrom":makeQuery(id+"F7.opPattern","COPY",BODY,{"derivedFrom":makeQuery(id+"F5.opPattern","COPY",BODY,{"derivedFrom":makeQuery(id+"F4.opPattern","COPY",BODY,{"derivedFrom":makeQuery(id+"F3.opPattern","COPY",BODY,{"derivedFrom":makeQuery(id+"F2.opPattern","COPY",BODY,{"derivedFrom":makeQuery(id+"F1.opRevolve","SWEPT_BODY",BODY,{"disambiguationData":[OSD([sQuery(id+"F0.wireOp",EDGE,"E1")])]}),"instanceName":"1"}),"instanceName":"1"}),"instanceName":"1"}),"instanceName":"1"}),"instanceName":"1"}),"instanceName":"1"}),"instanceName":"1"}),"instanceName":"1"});
            var Q372;
            Q372=makeQuery(id+"F10.opPattern","COPY",BODY,{"derivedFrom":makeQuery(id+"F9.opPattern","COPY",BODY,{"derivedFrom":makeQuery(id+"F8.opPattern","COPY",BODY,{"derivedFrom":makeQuery(id+"F7.opPattern","COPY",BODY,{"derivedFrom":makeQuery(id+"F6.opPattern","COPY",BODY,{"derivedFrom":makeQuery(id+"F1.opRevolve","SWEPT_BODY",BODY,{"disambiguationData":[OSD([sQuery(id+"F0.wireOp",EDGE,"E1")])]}),"instanceName":"1"}),"instanceName":"1"}),"instanceName":"1"}),"instanceName":"1"}),"instanceName":"1"});
            var Q373;
            Q373=makeQuery(id+"F10.opPattern","COPY",BODY,{"derivedFrom":makeQuery(id+"F9.opPattern","COPY",BODY,{"derivedFrom":makeQuery(id+"F8.opPattern","COPY",BODY,{"derivedFrom":makeQuery(id+"F7.opPattern","COPY",BODY,{"derivedFrom":makeQuery(id+"F6.opPattern","COPY",BODY,{"derivedFrom":makeQuery(id+"F2.opPattern","COPY",BODY,{"derivedFrom":makeQuery(id+"F1.opRevolve","SWEPT_BODY",BODY,{"disambiguationData":[OSD([sQuery(id+"F0.wireOp",EDGE,"E1")])]}),"instanceName":"1"}),"instanceName":"1"}),"instanceName":"1"}),"instanceName":"1"}),"instanceName":"1"}),"instanceName":"1"});
            var Q374;
            Q374=makeQuery(id+"F10.opPattern","COPY",BODY,{"derivedFrom":makeQuery(id+"F9.opPattern","COPY",BODY,{"derivedFrom":makeQuery(id+"F8.opPattern","COPY",BODY,{"derivedFrom":makeQuery(id+"F7.opPattern","COPY",BODY,{"derivedFrom":makeQuery(id+"F6.opPattern","COPY",BODY,{"derivedFrom":makeQuery(id+"F3.opPattern","COPY",BODY,{"derivedFrom":makeQuery(id+"F2.opPattern","COPY",BODY,{"derivedFrom":makeQuery(id+"F1.opRevolve","SWEPT_BODY",BODY,{"disambiguationData":[OSD([sQuery(id+"F0.wireOp",EDGE,"E1")])]}),"instanceName":"1"}),"instanceName":"1"}),"instanceName":"1"}),"instanceName":"1"}),"instanceName":"1"}),"instanceName":"1"}),"instanceName":"1"});
            var Q375;
            Q375=makeQuery(id+"F10.opPattern","COPY",BODY,{"derivedFrom":makeQuery(id+"F9.opPattern","COPY",BODY,{"derivedFrom":makeQuery(id+"F8.opPattern","COPY",BODY,{"derivedFrom":makeQuery(id+"F7.opPattern","COPY",BODY,{"derivedFrom":makeQuery(id+"F6.opPattern","COPY",BODY,{"derivedFrom":makeQuery(id+"F4.opPattern","COPY",BODY,{"derivedFrom":makeQuery(id+"F1.opRevolve","SWEPT_BODY",BODY,{"disambiguationData":[OSD([sQuery(id+"F0.wireOp",EDGE,"E1")])]}),"instanceName":"1"}),"instanceName":"1"}),"instanceName":"1"}),"instanceName":"1"}),"instanceName":"1"}),"instanceName":"1"});
            var Q376;
            Q376=makeQuery(id+"F10.opPattern","COPY",BODY,{"derivedFrom":makeQuery(id+"F9.opPattern","COPY",BODY,{"derivedFrom":makeQuery(id+"F8.opPattern","COPY",BODY,{"derivedFrom":makeQuery(id+"F7.opPattern","COPY",BODY,{"derivedFrom":makeQuery(id+"F6.opPattern","COPY",BODY,{"derivedFrom":makeQuery(id+"F4.opPattern","COPY",BODY,{"derivedFrom":makeQuery(id+"F2.opPattern","COPY",BODY,{"derivedFrom":makeQuery(id+"F1.opRevolve","SWEPT_BODY",BODY,{"disambiguationData":[OSD([sQuery(id+"F0.wireOp",EDGE,"E1")])]}),"instanceName":"1"}),"instanceName":"1"}),"instanceName":"1"}),"instanceName":"1"}),"instanceName":"1"}),"instanceName":"1"}),"instanceName":"1"});
            var Q377;
            Q377=makeQuery(id+"F10.opPattern","COPY",BODY,{"derivedFrom":makeQuery(id+"F9.opPattern","COPY",BODY,{"derivedFrom":makeQuery(id+"F8.opPattern","COPY",BODY,{"derivedFrom":makeQuery(id+"F7.opPattern","COPY",BODY,{"derivedFrom":makeQuery(id+"F6.opPattern","COPY",BODY,{"derivedFrom":makeQuery(id+"F4.opPattern","COPY",BODY,{"derivedFrom":makeQuery(id+"F3.opPattern","COPY",BODY,{"derivedFrom":makeQuery(id+"F2.opPattern","COPY",BODY,{"derivedFrom":makeQuery(id+"F1.opRevolve","SWEPT_BODY",BODY,{"disambiguationData":[OSD([sQuery(id+"F0.wireOp",EDGE,"E1")])]}),"instanceName":"1"}),"instanceName":"1"}),"instanceName":"1"}),"instanceName":"1"}),"instanceName":"1"}),"instanceName":"1"}),"instanceName":"1"}),"instanceName":"1"});
            var Q378;
            Q378=makeQuery(id+"F10.opPattern","COPY",BODY,{"derivedFrom":makeQuery(id+"F9.opPattern","COPY",BODY,{"derivedFrom":makeQuery(id+"F8.opPattern","COPY",BODY,{"derivedFrom":makeQuery(id+"F7.opPattern","COPY",BODY,{"derivedFrom":makeQuery(id+"F6.opPattern","COPY",BODY,{"derivedFrom":makeQuery(id+"F5.opPattern","COPY",BODY,{"derivedFrom":makeQuery(id+"F1.opRevolve","SWEPT_BODY",BODY,{"disambiguationData":[OSD([sQuery(id+"F0.wireOp",EDGE,"E1")])]}),"instanceName":"1"}),"instanceName":"1"}),"instanceName":"1"}),"instanceName":"1"}),"instanceName":"1"}),"instanceName":"1"});
            var Q379;
            Q379=makeQuery(id+"F10.opPattern","COPY",BODY,{"derivedFrom":makeQuery(id+"F9.opPattern","COPY",BODY,{"derivedFrom":makeQuery(id+"F8.opPattern","COPY",BODY,{"derivedFrom":makeQuery(id+"F7.opPattern","COPY",BODY,{"derivedFrom":makeQuery(id+"F6.opPattern","COPY",BODY,{"derivedFrom":makeQuery(id+"F5.opPattern","COPY",BODY,{"derivedFrom":makeQuery(id+"F2.opPattern","COPY",BODY,{"derivedFrom":makeQuery(id+"F1.opRevolve","SWEPT_BODY",BODY,{"disambiguationData":[OSD([sQuery(id+"F0.wireOp",EDGE,"E1")])]}),"instanceName":"1"}),"instanceName":"1"}),"instanceName":"1"}),"instanceName":"1"}),"instanceName":"1"}),"instanceName":"1"}),"instanceName":"1"});
            var Q380;
            Q380=makeQuery(id+"F10.opPattern","COPY",BODY,{"derivedFrom":makeQuery(id+"F9.opPattern","COPY",BODY,{"derivedFrom":makeQuery(id+"F8.opPattern","COPY",BODY,{"derivedFrom":makeQuery(id+"F7.opPattern","COPY",BODY,{"derivedFrom":makeQuery(id+"F6.opPattern","COPY",BODY,{"derivedFrom":makeQuery(id+"F5.opPattern","COPY",BODY,{"derivedFrom":makeQuery(id+"F3.opPattern","COPY",BODY,{"derivedFrom":makeQuery(id+"F2.opPattern","COPY",BODY,{"derivedFrom":makeQuery(id+"F1.opRevolve","SWEPT_BODY",BODY,{"disambiguationData":[OSD([sQuery(id+"F0.wireOp",EDGE,"E1")])]}),"instanceName":"1"}),"instanceName":"1"}),"instanceName":"1"}),"instanceName":"1"}),"instanceName":"1"}),"instanceName":"1"}),"instanceName":"1"}),"instanceName":"1"});
            var Q381;
            Q381=makeQuery(id+"F10.opPattern","COPY",BODY,{"derivedFrom":makeQuery(id+"F9.opPattern","COPY",BODY,{"derivedFrom":makeQuery(id+"F8.opPattern","COPY",BODY,{"derivedFrom":makeQuery(id+"F7.opPattern","COPY",BODY,{"derivedFrom":makeQuery(id+"F6.opPattern","COPY",BODY,{"derivedFrom":makeQuery(id+"F5.opPattern","COPY",BODY,{"derivedFrom":makeQuery(id+"F4.opPattern","COPY",BODY,{"derivedFrom":makeQuery(id+"F1.opRevolve","SWEPT_BODY",BODY,{"disambiguationData":[OSD([sQuery(id+"F0.wireOp",EDGE,"E1")])]}),"instanceName":"1"}),"instanceName":"1"}),"instanceName":"1"}),"instanceName":"1"}),"instanceName":"1"}),"instanceName":"1"}),"instanceName":"1"});
            var Q382;
            Q382=makeQuery(id+"F10.opPattern","COPY",BODY,{"derivedFrom":makeQuery(id+"F9.opPattern","COPY",BODY,{"derivedFrom":makeQuery(id+"F8.opPattern","COPY",BODY,{"derivedFrom":makeQuery(id+"F7.opPattern","COPY",BODY,{"derivedFrom":makeQuery(id+"F6.opPattern","COPY",BODY,{"derivedFrom":makeQuery(id+"F5.opPattern","COPY",BODY,{"derivedFrom":makeQuery(id+"F4.opPattern","COPY",BODY,{"derivedFrom":makeQuery(id+"F2.opPattern","COPY",BODY,{"derivedFrom":makeQuery(id+"F1.opRevolve","SWEPT_BODY",BODY,{"disambiguationData":[OSD([sQuery(id+"F0.wireOp",EDGE,"E1")])]}),"instanceName":"1"}),"instanceName":"1"}),"instanceName":"1"}),"instanceName":"1"}),"instanceName":"1"}),"instanceName":"1"}),"instanceName":"1"}),"instanceName":"1"});
            var Q383;
            Q383=makeQuery(id+"F10.opPattern","COPY",BODY,{"derivedFrom":makeQuery(id+"F9.opPattern","COPY",BODY,{"derivedFrom":makeQuery(id+"F8.opPattern","COPY",BODY,{"derivedFrom":makeQuery(id+"F7.opPattern","COPY",BODY,{"derivedFrom":makeQuery(id+"F6.opPattern","COPY",BODY,{"derivedFrom":makeQuery(id+"F5.opPattern","COPY",BODY,{"derivedFrom":makeQuery(id+"F4.opPattern","COPY",BODY,{"derivedFrom":makeQuery(id+"F3.opPattern","COPY",BODY,{"derivedFrom":makeQuery(id+"F2.opPattern","COPY",BODY,{"derivedFrom":makeQuery(id+"F1.opRevolve","SWEPT_BODY",BODY,{"disambiguationData":[OSD([sQuery(id+"F0.wireOp",EDGE,"E1")])]}),"instanceName":"1"}),"instanceName":"1"}),"instanceName":"1"}),"instanceName":"1"}),"instanceName":"1"}),"instanceName":"1"}),"instanceName":"1"}),"instanceName":"1"}),"instanceName":"1"});
            var Q384;
            Q384=makeQuery(id+"F11.opPattern","COPY",BODY,{"derivedFrom":makeQuery(id+"F1.opRevolve","SWEPT_BODY",BODY,{"disambiguationData":[OSD([sQuery(id+"F0.wireOp",EDGE,"E1")])]}),"instanceName":"1"});
            var Q385;
            Q385=makeQuery(id+"F11.opPattern","COPY",BODY,{"derivedFrom":makeQuery(id+"F2.opPattern","COPY",BODY,{"derivedFrom":makeQuery(id+"F1.opRevolve","SWEPT_BODY",BODY,{"disambiguationData":[OSD([sQuery(id+"F0.wireOp",EDGE,"E1")])]}),"instanceName":"1"}),"instanceName":"1"});
            var Q386;
            Q386=makeQuery(id+"F11.opPattern","COPY",BODY,{"derivedFrom":makeQuery(id+"F3.opPattern","COPY",BODY,{"derivedFrom":makeQuery(id+"F2.opPattern","COPY",BODY,{"derivedFrom":makeQuery(id+"F1.opRevolve","SWEPT_BODY",BODY,{"disambiguationData":[OSD([sQuery(id+"F0.wireOp",EDGE,"E1")])]}),"instanceName":"1"}),"instanceName":"1"}),"instanceName":"1"});
            var Q387;
            Q387=makeQuery(id+"F11.opPattern","COPY",BODY,{"derivedFrom":makeQuery(id+"F4.opPattern","COPY",BODY,{"derivedFrom":makeQuery(id+"F1.opRevolve","SWEPT_BODY",BODY,{"disambiguationData":[OSD([sQuery(id+"F0.wireOp",EDGE,"E1")])]}),"instanceName":"1"}),"instanceName":"1"});
            var Q388;
            Q388=makeQuery(id+"F11.opPattern","COPY",BODY,{"derivedFrom":makeQuery(id+"F4.opPattern","COPY",BODY,{"derivedFrom":makeQuery(id+"F2.opPattern","COPY",BODY,{"derivedFrom":makeQuery(id+"F1.opRevolve","SWEPT_BODY",BODY,{"disambiguationData":[OSD([sQuery(id+"F0.wireOp",EDGE,"E1")])]}),"instanceName":"1"}),"instanceName":"1"}),"instanceName":"1"});
            var Q389;
            Q389=makeQuery(id+"F11.opPattern","COPY",BODY,{"derivedFrom":makeQuery(id+"F4.opPattern","COPY",BODY,{"derivedFrom":makeQuery(id+"F3.opPattern","COPY",BODY,{"derivedFrom":makeQuery(id+"F2.opPattern","COPY",BODY,{"derivedFrom":makeQuery(id+"F1.opRevolve","SWEPT_BODY",BODY,{"disambiguationData":[OSD([sQuery(id+"F0.wireOp",EDGE,"E1")])]}),"instanceName":"1"}),"instanceName":"1"}),"instanceName":"1"}),"instanceName":"1"});
            var Q390;
            Q390=makeQuery(id+"F11.opPattern","COPY",BODY,{"derivedFrom":makeQuery(id+"F5.opPattern","COPY",BODY,{"derivedFrom":makeQuery(id+"F1.opRevolve","SWEPT_BODY",BODY,{"disambiguationData":[OSD([sQuery(id+"F0.wireOp",EDGE,"E1")])]}),"instanceName":"1"}),"instanceName":"1"});
            var Q391;
            Q391=makeQuery(id+"F11.opPattern","COPY",BODY,{"derivedFrom":makeQuery(id+"F5.opPattern","COPY",BODY,{"derivedFrom":makeQuery(id+"F2.opPattern","COPY",BODY,{"derivedFrom":makeQuery(id+"F1.opRevolve","SWEPT_BODY",BODY,{"disambiguationData":[OSD([sQuery(id+"F0.wireOp",EDGE,"E1")])]}),"instanceName":"1"}),"instanceName":"1"}),"instanceName":"1"});
            var Q392;
            Q392=makeQuery(id+"F11.opPattern","COPY",BODY,{"derivedFrom":makeQuery(id+"F5.opPattern","COPY",BODY,{"derivedFrom":makeQuery(id+"F3.opPattern","COPY",BODY,{"derivedFrom":makeQuery(id+"F2.opPattern","COPY",BODY,{"derivedFrom":makeQuery(id+"F1.opRevolve","SWEPT_BODY",BODY,{"disambiguationData":[OSD([sQuery(id+"F0.wireOp",EDGE,"E1")])]}),"instanceName":"1"}),"instanceName":"1"}),"instanceName":"1"}),"instanceName":"1"});
            var Q393;
            Q393=makeQuery(id+"F11.opPattern","COPY",BODY,{"derivedFrom":makeQuery(id+"F5.opPattern","COPY",BODY,{"derivedFrom":makeQuery(id+"F4.opPattern","COPY",BODY,{"derivedFrom":makeQuery(id+"F1.opRevolve","SWEPT_BODY",BODY,{"disambiguationData":[OSD([sQuery(id+"F0.wireOp",EDGE,"E1")])]}),"instanceName":"1"}),"instanceName":"1"}),"instanceName":"1"});
            var Q394;
            Q394=makeQuery(id+"F11.opPattern","COPY",BODY,{"derivedFrom":makeQuery(id+"F5.opPattern","COPY",BODY,{"derivedFrom":makeQuery(id+"F4.opPattern","COPY",BODY,{"derivedFrom":makeQuery(id+"F2.opPattern","COPY",BODY,{"derivedFrom":makeQuery(id+"F1.opRevolve","SWEPT_BODY",BODY,{"disambiguationData":[OSD([sQuery(id+"F0.wireOp",EDGE,"E1")])]}),"instanceName":"1"}),"instanceName":"1"}),"instanceName":"1"}),"instanceName":"1"});
            var Q395;
            Q395=makeQuery(id+"F11.opPattern","COPY",BODY,{"derivedFrom":makeQuery(id+"F5.opPattern","COPY",BODY,{"derivedFrom":makeQuery(id+"F4.opPattern","COPY",BODY,{"derivedFrom":makeQuery(id+"F3.opPattern","COPY",BODY,{"derivedFrom":makeQuery(id+"F2.opPattern","COPY",BODY,{"derivedFrom":makeQuery(id+"F1.opRevolve","SWEPT_BODY",BODY,{"disambiguationData":[OSD([sQuery(id+"F0.wireOp",EDGE,"E1")])]}),"instanceName":"1"}),"instanceName":"1"}),"instanceName":"1"}),"instanceName":"1"}),"instanceName":"1"});
            var Q396;
            Q396=makeQuery(id+"F11.opPattern","COPY",BODY,{"derivedFrom":makeQuery(id+"F6.opPattern","COPY",BODY,{"derivedFrom":makeQuery(id+"F1.opRevolve","SWEPT_BODY",BODY,{"disambiguationData":[OSD([sQuery(id+"F0.wireOp",EDGE,"E1")])]}),"instanceName":"1"}),"instanceName":"1"});
            var Q397;
            Q397=makeQuery(id+"F11.opPattern","COPY",BODY,{"derivedFrom":makeQuery(id+"F6.opPattern","COPY",BODY,{"derivedFrom":makeQuery(id+"F2.opPattern","COPY",BODY,{"derivedFrom":makeQuery(id+"F1.opRevolve","SWEPT_BODY",BODY,{"disambiguationData":[OSD([sQuery(id+"F0.wireOp",EDGE,"E1")])]}),"instanceName":"1"}),"instanceName":"1"}),"instanceName":"1"});
            var Q398;
            Q398=makeQuery(id+"F11.opPattern","COPY",BODY,{"derivedFrom":makeQuery(id+"F6.opPattern","COPY",BODY,{"derivedFrom":makeQuery(id+"F3.opPattern","COPY",BODY,{"derivedFrom":makeQuery(id+"F2.opPattern","COPY",BODY,{"derivedFrom":makeQuery(id+"F1.opRevolve","SWEPT_BODY",BODY,{"disambiguationData":[OSD([sQuery(id+"F0.wireOp",EDGE,"E1")])]}),"instanceName":"1"}),"instanceName":"1"}),"instanceName":"1"}),"instanceName":"1"});
            var Q399;
            Q399=makeQuery(id+"F11.opPattern","COPY",BODY,{"derivedFrom":makeQuery(id+"F6.opPattern","COPY",BODY,{"derivedFrom":makeQuery(id+"F4.opPattern","COPY",BODY,{"derivedFrom":makeQuery(id+"F1.opRevolve","SWEPT_BODY",BODY,{"disambiguationData":[OSD([sQuery(id+"F0.wireOp",EDGE,"E1")])]}),"instanceName":"1"}),"instanceName":"1"}),"instanceName":"1"});
            var Q400;
            Q400=makeQuery(id+"F11.opPattern","COPY",BODY,{"derivedFrom":makeQuery(id+"F6.opPattern","COPY",BODY,{"derivedFrom":makeQuery(id+"F4.opPattern","COPY",BODY,{"derivedFrom":makeQuery(id+"F2.opPattern","COPY",BODY,{"derivedFrom":makeQuery(id+"F1.opRevolve","SWEPT_BODY",BODY,{"disambiguationData":[OSD([sQuery(id+"F0.wireOp",EDGE,"E1")])]}),"instanceName":"1"}),"instanceName":"1"}),"instanceName":"1"}),"instanceName":"1"});
            var Q401;
            Q401=makeQuery(id+"F11.opPattern","COPY",BODY,{"derivedFrom":makeQuery(id+"F6.opPattern","COPY",BODY,{"derivedFrom":makeQuery(id+"F4.opPattern","COPY",BODY,{"derivedFrom":makeQuery(id+"F3.opPattern","COPY",BODY,{"derivedFrom":makeQuery(id+"F2.opPattern","COPY",BODY,{"derivedFrom":makeQuery(id+"F1.opRevolve","SWEPT_BODY",BODY,{"disambiguationData":[OSD([sQuery(id+"F0.wireOp",EDGE,"E1")])]}),"instanceName":"1"}),"instanceName":"1"}),"instanceName":"1"}),"instanceName":"1"}),"instanceName":"1"});
            var Q402;
            Q402=makeQuery(id+"F11.opPattern","COPY",BODY,{"derivedFrom":makeQuery(id+"F6.opPattern","COPY",BODY,{"derivedFrom":makeQuery(id+"F5.opPattern","COPY",BODY,{"derivedFrom":makeQuery(id+"F1.opRevolve","SWEPT_BODY",BODY,{"disambiguationData":[OSD([sQuery(id+"F0.wireOp",EDGE,"E1")])]}),"instanceName":"1"}),"instanceName":"1"}),"instanceName":"1"});
            var Q403;
            Q403=makeQuery(id+"F11.opPattern","COPY",BODY,{"derivedFrom":makeQuery(id+"F6.opPattern","COPY",BODY,{"derivedFrom":makeQuery(id+"F5.opPattern","COPY",BODY,{"derivedFrom":makeQuery(id+"F2.opPattern","COPY",BODY,{"derivedFrom":makeQuery(id+"F1.opRevolve","SWEPT_BODY",BODY,{"disambiguationData":[OSD([sQuery(id+"F0.wireOp",EDGE,"E1")])]}),"instanceName":"1"}),"instanceName":"1"}),"instanceName":"1"}),"instanceName":"1"});
            var Q404;
            Q404=makeQuery(id+"F11.opPattern","COPY",BODY,{"derivedFrom":makeQuery(id+"F6.opPattern","COPY",BODY,{"derivedFrom":makeQuery(id+"F5.opPattern","COPY",BODY,{"derivedFrom":makeQuery(id+"F3.opPattern","COPY",BODY,{"derivedFrom":makeQuery(id+"F2.opPattern","COPY",BODY,{"derivedFrom":makeQuery(id+"F1.opRevolve","SWEPT_BODY",BODY,{"disambiguationData":[OSD([sQuery(id+"F0.wireOp",EDGE,"E1")])]}),"instanceName":"1"}),"instanceName":"1"}),"instanceName":"1"}),"instanceName":"1"}),"instanceName":"1"});
            var Q405;
            Q405=makeQuery(id+"F11.opPattern","COPY",BODY,{"derivedFrom":makeQuery(id+"F6.opPattern","COPY",BODY,{"derivedFrom":makeQuery(id+"F5.opPattern","COPY",BODY,{"derivedFrom":makeQuery(id+"F4.opPattern","COPY",BODY,{"derivedFrom":makeQuery(id+"F1.opRevolve","SWEPT_BODY",BODY,{"disambiguationData":[OSD([sQuery(id+"F0.wireOp",EDGE,"E1")])]}),"instanceName":"1"}),"instanceName":"1"}),"instanceName":"1"}),"instanceName":"1"});
            var Q406;
            Q406=makeQuery(id+"F11.opPattern","COPY",BODY,{"derivedFrom":makeQuery(id+"F6.opPattern","COPY",BODY,{"derivedFrom":makeQuery(id+"F5.opPattern","COPY",BODY,{"derivedFrom":makeQuery(id+"F4.opPattern","COPY",BODY,{"derivedFrom":makeQuery(id+"F2.opPattern","COPY",BODY,{"derivedFrom":makeQuery(id+"F1.opRevolve","SWEPT_BODY",BODY,{"disambiguationData":[OSD([sQuery(id+"F0.wireOp",EDGE,"E1")])]}),"instanceName":"1"}),"instanceName":"1"}),"instanceName":"1"}),"instanceName":"1"}),"instanceName":"1"});
            var Q407;
            Q407=makeQuery(id+"F11.opPattern","COPY",BODY,{"derivedFrom":makeQuery(id+"F6.opPattern","COPY",BODY,{"derivedFrom":makeQuery(id+"F5.opPattern","COPY",BODY,{"derivedFrom":makeQuery(id+"F4.opPattern","COPY",BODY,{"derivedFrom":makeQuery(id+"F3.opPattern","COPY",BODY,{"derivedFrom":makeQuery(id+"F2.opPattern","COPY",BODY,{"derivedFrom":makeQuery(id+"F1.opRevolve","SWEPT_BODY",BODY,{"disambiguationData":[OSD([sQuery(id+"F0.wireOp",EDGE,"E1")])]}),"instanceName":"1"}),"instanceName":"1"}),"instanceName":"1"}),"instanceName":"1"}),"instanceName":"1"}),"instanceName":"1"});
            var Q408;
            Q408=makeQuery(id+"F11.opPattern","COPY",BODY,{"derivedFrom":makeQuery(id+"F7.opPattern","COPY",BODY,{"derivedFrom":makeQuery(id+"F1.opRevolve","SWEPT_BODY",BODY,{"disambiguationData":[OSD([sQuery(id+"F0.wireOp",EDGE,"E1")])]}),"instanceName":"1"}),"instanceName":"1"});
            var Q409;
            Q409=makeQuery(id+"F11.opPattern","COPY",BODY,{"derivedFrom":makeQuery(id+"F7.opPattern","COPY",BODY,{"derivedFrom":makeQuery(id+"F2.opPattern","COPY",BODY,{"derivedFrom":makeQuery(id+"F1.opRevolve","SWEPT_BODY",BODY,{"disambiguationData":[OSD([sQuery(id+"F0.wireOp",EDGE,"E1")])]}),"instanceName":"1"}),"instanceName":"1"}),"instanceName":"1"});
            var Q410;
            Q410=makeQuery(id+"F11.opPattern","COPY",BODY,{"derivedFrom":makeQuery(id+"F7.opPattern","COPY",BODY,{"derivedFrom":makeQuery(id+"F3.opPattern","COPY",BODY,{"derivedFrom":makeQuery(id+"F2.opPattern","COPY",BODY,{"derivedFrom":makeQuery(id+"F1.opRevolve","SWEPT_BODY",BODY,{"disambiguationData":[OSD([sQuery(id+"F0.wireOp",EDGE,"E1")])]}),"instanceName":"1"}),"instanceName":"1"}),"instanceName":"1"}),"instanceName":"1"});
            var Q411;
            Q411=makeQuery(id+"F11.opPattern","COPY",BODY,{"derivedFrom":makeQuery(id+"F7.opPattern","COPY",BODY,{"derivedFrom":makeQuery(id+"F4.opPattern","COPY",BODY,{"derivedFrom":makeQuery(id+"F1.opRevolve","SWEPT_BODY",BODY,{"disambiguationData":[OSD([sQuery(id+"F0.wireOp",EDGE,"E1")])]}),"instanceName":"1"}),"instanceName":"1"}),"instanceName":"1"});
            var Q412;
            Q412=makeQuery(id+"F11.opPattern","COPY",BODY,{"derivedFrom":makeQuery(id+"F7.opPattern","COPY",BODY,{"derivedFrom":makeQuery(id+"F4.opPattern","COPY",BODY,{"derivedFrom":makeQuery(id+"F2.opPattern","COPY",BODY,{"derivedFrom":makeQuery(id+"F1.opRevolve","SWEPT_BODY",BODY,{"disambiguationData":[OSD([sQuery(id+"F0.wireOp",EDGE,"E1")])]}),"instanceName":"1"}),"instanceName":"1"}),"instanceName":"1"}),"instanceName":"1"});
            var Q413;
            Q413=makeQuery(id+"F11.opPattern","COPY",BODY,{"derivedFrom":makeQuery(id+"F7.opPattern","COPY",BODY,{"derivedFrom":makeQuery(id+"F4.opPattern","COPY",BODY,{"derivedFrom":makeQuery(id+"F3.opPattern","COPY",BODY,{"derivedFrom":makeQuery(id+"F2.opPattern","COPY",BODY,{"derivedFrom":makeQuery(id+"F1.opRevolve","SWEPT_BODY",BODY,{"disambiguationData":[OSD([sQuery(id+"F0.wireOp",EDGE,"E1")])]}),"instanceName":"1"}),"instanceName":"1"}),"instanceName":"1"}),"instanceName":"1"}),"instanceName":"1"});
            var Q414;
            Q414=makeQuery(id+"F11.opPattern","COPY",BODY,{"derivedFrom":makeQuery(id+"F7.opPattern","COPY",BODY,{"derivedFrom":makeQuery(id+"F5.opPattern","COPY",BODY,{"derivedFrom":makeQuery(id+"F1.opRevolve","SWEPT_BODY",BODY,{"disambiguationData":[OSD([sQuery(id+"F0.wireOp",EDGE,"E1")])]}),"instanceName":"1"}),"instanceName":"1"}),"instanceName":"1"});
            var Q415;
            Q415=makeQuery(id+"F11.opPattern","COPY",BODY,{"derivedFrom":makeQuery(id+"F7.opPattern","COPY",BODY,{"derivedFrom":makeQuery(id+"F5.opPattern","COPY",BODY,{"derivedFrom":makeQuery(id+"F2.opPattern","COPY",BODY,{"derivedFrom":makeQuery(id+"F1.opRevolve","SWEPT_BODY",BODY,{"disambiguationData":[OSD([sQuery(id+"F0.wireOp",EDGE,"E1")])]}),"instanceName":"1"}),"instanceName":"1"}),"instanceName":"1"}),"instanceName":"1"});
            var Q416;
            Q416=makeQuery(id+"F11.opPattern","COPY",BODY,{"derivedFrom":makeQuery(id+"F7.opPattern","COPY",BODY,{"derivedFrom":makeQuery(id+"F5.opPattern","COPY",BODY,{"derivedFrom":makeQuery(id+"F3.opPattern","COPY",BODY,{"derivedFrom":makeQuery(id+"F2.opPattern","COPY",BODY,{"derivedFrom":makeQuery(id+"F1.opRevolve","SWEPT_BODY",BODY,{"disambiguationData":[OSD([sQuery(id+"F0.wireOp",EDGE,"E1")])]}),"instanceName":"1"}),"instanceName":"1"}),"instanceName":"1"}),"instanceName":"1"}),"instanceName":"1"});
            var Q417;
            Q417=makeQuery(id+"F11.opPattern","COPY",BODY,{"derivedFrom":makeQuery(id+"F7.opPattern","COPY",BODY,{"derivedFrom":makeQuery(id+"F5.opPattern","COPY",BODY,{"derivedFrom":makeQuery(id+"F4.opPattern","COPY",BODY,{"derivedFrom":makeQuery(id+"F1.opRevolve","SWEPT_BODY",BODY,{"disambiguationData":[OSD([sQuery(id+"F0.wireOp",EDGE,"E1")])]}),"instanceName":"1"}),"instanceName":"1"}),"instanceName":"1"}),"instanceName":"1"});
            var Q418;
            Q418=makeQuery(id+"F11.opPattern","COPY",BODY,{"derivedFrom":makeQuery(id+"F7.opPattern","COPY",BODY,{"derivedFrom":makeQuery(id+"F5.opPattern","COPY",BODY,{"derivedFrom":makeQuery(id+"F4.opPattern","COPY",BODY,{"derivedFrom":makeQuery(id+"F2.opPattern","COPY",BODY,{"derivedFrom":makeQuery(id+"F1.opRevolve","SWEPT_BODY",BODY,{"disambiguationData":[OSD([sQuery(id+"F0.wireOp",EDGE,"E1")])]}),"instanceName":"1"}),"instanceName":"1"}),"instanceName":"1"}),"instanceName":"1"}),"instanceName":"1"});
            var Q419;
            Q419=makeQuery(id+"F11.opPattern","COPY",BODY,{"derivedFrom":makeQuery(id+"F7.opPattern","COPY",BODY,{"derivedFrom":makeQuery(id+"F5.opPattern","COPY",BODY,{"derivedFrom":makeQuery(id+"F4.opPattern","COPY",BODY,{"derivedFrom":makeQuery(id+"F3.opPattern","COPY",BODY,{"derivedFrom":makeQuery(id+"F2.opPattern","COPY",BODY,{"derivedFrom":makeQuery(id+"F1.opRevolve","SWEPT_BODY",BODY,{"disambiguationData":[OSD([sQuery(id+"F0.wireOp",EDGE,"E1")])]}),"instanceName":"1"}),"instanceName":"1"}),"instanceName":"1"}),"instanceName":"1"}),"instanceName":"1"}),"instanceName":"1"});
            var Q420;
            Q420=makeQuery(id+"F11.opPattern","COPY",BODY,{"derivedFrom":makeQuery(id+"F7.opPattern","COPY",BODY,{"derivedFrom":makeQuery(id+"F6.opPattern","COPY",BODY,{"derivedFrom":makeQuery(id+"F1.opRevolve","SWEPT_BODY",BODY,{"disambiguationData":[OSD([sQuery(id+"F0.wireOp",EDGE,"E1")])]}),"instanceName":"1"}),"instanceName":"1"}),"instanceName":"1"});
            var Q421;
            Q421=makeQuery(id+"F11.opPattern","COPY",BODY,{"derivedFrom":makeQuery(id+"F7.opPattern","COPY",BODY,{"derivedFrom":makeQuery(id+"F6.opPattern","COPY",BODY,{"derivedFrom":makeQuery(id+"F2.opPattern","COPY",BODY,{"derivedFrom":makeQuery(id+"F1.opRevolve","SWEPT_BODY",BODY,{"disambiguationData":[OSD([sQuery(id+"F0.wireOp",EDGE,"E1")])]}),"instanceName":"1"}),"instanceName":"1"}),"instanceName":"1"}),"instanceName":"1"});
            var Q422;
            Q422=makeQuery(id+"F11.opPattern","COPY",BODY,{"derivedFrom":makeQuery(id+"F7.opPattern","COPY",BODY,{"derivedFrom":makeQuery(id+"F6.opPattern","COPY",BODY,{"derivedFrom":makeQuery(id+"F3.opPattern","COPY",BODY,{"derivedFrom":makeQuery(id+"F2.opPattern","COPY",BODY,{"derivedFrom":makeQuery(id+"F1.opRevolve","SWEPT_BODY",BODY,{"disambiguationData":[OSD([sQuery(id+"F0.wireOp",EDGE,"E1")])]}),"instanceName":"1"}),"instanceName":"1"}),"instanceName":"1"}),"instanceName":"1"}),"instanceName":"1"});
            var Q423;
            Q423=makeQuery(id+"F11.opPattern","COPY",BODY,{"derivedFrom":makeQuery(id+"F7.opPattern","COPY",BODY,{"derivedFrom":makeQuery(id+"F6.opPattern","COPY",BODY,{"derivedFrom":makeQuery(id+"F4.opPattern","COPY",BODY,{"derivedFrom":makeQuery(id+"F1.opRevolve","SWEPT_BODY",BODY,{"disambiguationData":[OSD([sQuery(id+"F0.wireOp",EDGE,"E1")])]}),"instanceName":"1"}),"instanceName":"1"}),"instanceName":"1"}),"instanceName":"1"});
            var Q424;
            Q424=makeQuery(id+"F11.opPattern","COPY",BODY,{"derivedFrom":makeQuery(id+"F7.opPattern","COPY",BODY,{"derivedFrom":makeQuery(id+"F6.opPattern","COPY",BODY,{"derivedFrom":makeQuery(id+"F4.opPattern","COPY",BODY,{"derivedFrom":makeQuery(id+"F2.opPattern","COPY",BODY,{"derivedFrom":makeQuery(id+"F1.opRevolve","SWEPT_BODY",BODY,{"disambiguationData":[OSD([sQuery(id+"F0.wireOp",EDGE,"E1")])]}),"instanceName":"1"}),"instanceName":"1"}),"instanceName":"1"}),"instanceName":"1"}),"instanceName":"1"});
            var Q425;
            Q425=makeQuery(id+"F11.opPattern","COPY",BODY,{"derivedFrom":makeQuery(id+"F7.opPattern","COPY",BODY,{"derivedFrom":makeQuery(id+"F6.opPattern","COPY",BODY,{"derivedFrom":makeQuery(id+"F4.opPattern","COPY",BODY,{"derivedFrom":makeQuery(id+"F3.opPattern","COPY",BODY,{"derivedFrom":makeQuery(id+"F2.opPattern","COPY",BODY,{"derivedFrom":makeQuery(id+"F1.opRevolve","SWEPT_BODY",BODY,{"disambiguationData":[OSD([sQuery(id+"F0.wireOp",EDGE,"E1")])]}),"instanceName":"1"}),"instanceName":"1"}),"instanceName":"1"}),"instanceName":"1"}),"instanceName":"1"}),"instanceName":"1"});
            var Q426;
            Q426=makeQuery(id+"F11.opPattern","COPY",BODY,{"derivedFrom":makeQuery(id+"F7.opPattern","COPY",BODY,{"derivedFrom":makeQuery(id+"F6.opPattern","COPY",BODY,{"derivedFrom":makeQuery(id+"F5.opPattern","COPY",BODY,{"derivedFrom":makeQuery(id+"F1.opRevolve","SWEPT_BODY",BODY,{"disambiguationData":[OSD([sQuery(id+"F0.wireOp",EDGE,"E1")])]}),"instanceName":"1"}),"instanceName":"1"}),"instanceName":"1"}),"instanceName":"1"});
            var Q427;
            Q427=makeQuery(id+"F11.opPattern","COPY",BODY,{"derivedFrom":makeQuery(id+"F7.opPattern","COPY",BODY,{"derivedFrom":makeQuery(id+"F6.opPattern","COPY",BODY,{"derivedFrom":makeQuery(id+"F5.opPattern","COPY",BODY,{"derivedFrom":makeQuery(id+"F2.opPattern","COPY",BODY,{"derivedFrom":makeQuery(id+"F1.opRevolve","SWEPT_BODY",BODY,{"disambiguationData":[OSD([sQuery(id+"F0.wireOp",EDGE,"E1")])]}),"instanceName":"1"}),"instanceName":"1"}),"instanceName":"1"}),"instanceName":"1"}),"instanceName":"1"});
            var Q428;
            Q428=makeQuery(id+"F11.opPattern","COPY",BODY,{"derivedFrom":makeQuery(id+"F7.opPattern","COPY",BODY,{"derivedFrom":makeQuery(id+"F6.opPattern","COPY",BODY,{"derivedFrom":makeQuery(id+"F5.opPattern","COPY",BODY,{"derivedFrom":makeQuery(id+"F3.opPattern","COPY",BODY,{"derivedFrom":makeQuery(id+"F2.opPattern","COPY",BODY,{"derivedFrom":makeQuery(id+"F1.opRevolve","SWEPT_BODY",BODY,{"disambiguationData":[OSD([sQuery(id+"F0.wireOp",EDGE,"E1")])]}),"instanceName":"1"}),"instanceName":"1"}),"instanceName":"1"}),"instanceName":"1"}),"instanceName":"1"}),"instanceName":"1"});
            var Q429;
            Q429=makeQuery(id+"F11.opPattern","COPY",BODY,{"derivedFrom":makeQuery(id+"F7.opPattern","COPY",BODY,{"derivedFrom":makeQuery(id+"F6.opPattern","COPY",BODY,{"derivedFrom":makeQuery(id+"F5.opPattern","COPY",BODY,{"derivedFrom":makeQuery(id+"F4.opPattern","COPY",BODY,{"derivedFrom":makeQuery(id+"F1.opRevolve","SWEPT_BODY",BODY,{"disambiguationData":[OSD([sQuery(id+"F0.wireOp",EDGE,"E1")])]}),"instanceName":"1"}),"instanceName":"1"}),"instanceName":"1"}),"instanceName":"1"}),"instanceName":"1"});
            var Q430;
            Q430=makeQuery(id+"F11.opPattern","COPY",BODY,{"derivedFrom":makeQuery(id+"F7.opPattern","COPY",BODY,{"derivedFrom":makeQuery(id+"F6.opPattern","COPY",BODY,{"derivedFrom":makeQuery(id+"F5.opPattern","COPY",BODY,{"derivedFrom":makeQuery(id+"F4.opPattern","COPY",BODY,{"derivedFrom":makeQuery(id+"F2.opPattern","COPY",BODY,{"derivedFrom":makeQuery(id+"F1.opRevolve","SWEPT_BODY",BODY,{"disambiguationData":[OSD([sQuery(id+"F0.wireOp",EDGE,"E1")])]}),"instanceName":"1"}),"instanceName":"1"}),"instanceName":"1"}),"instanceName":"1"}),"instanceName":"1"}),"instanceName":"1"});
            var Q431;
            Q431=makeQuery(id+"F11.opPattern","COPY",BODY,{"derivedFrom":makeQuery(id+"F7.opPattern","COPY",BODY,{"derivedFrom":makeQuery(id+"F6.opPattern","COPY",BODY,{"derivedFrom":makeQuery(id+"F5.opPattern","COPY",BODY,{"derivedFrom":makeQuery(id+"F4.opPattern","COPY",BODY,{"derivedFrom":makeQuery(id+"F3.opPattern","COPY",BODY,{"derivedFrom":makeQuery(id+"F2.opPattern","COPY",BODY,{"derivedFrom":makeQuery(id+"F1.opRevolve","SWEPT_BODY",BODY,{"disambiguationData":[OSD([sQuery(id+"F0.wireOp",EDGE,"E1")])]}),"instanceName":"1"}),"instanceName":"1"}),"instanceName":"1"}),"instanceName":"1"}),"instanceName":"1"}),"instanceName":"1"}),"instanceName":"1"});
            var Q432;
            Q432=makeQuery(id+"F11.opPattern","COPY",BODY,{"derivedFrom":makeQuery(id+"F8.opPattern","COPY",BODY,{"derivedFrom":makeQuery(id+"F1.opRevolve","SWEPT_BODY",BODY,{"disambiguationData":[OSD([sQuery(id+"F0.wireOp",EDGE,"E1")])]}),"instanceName":"1"}),"instanceName":"1"});
            var Q433;
            Q433=makeQuery(id+"F11.opPattern","COPY",BODY,{"derivedFrom":makeQuery(id+"F8.opPattern","COPY",BODY,{"derivedFrom":makeQuery(id+"F2.opPattern","COPY",BODY,{"derivedFrom":makeQuery(id+"F1.opRevolve","SWEPT_BODY",BODY,{"disambiguationData":[OSD([sQuery(id+"F0.wireOp",EDGE,"E1")])]}),"instanceName":"1"}),"instanceName":"1"}),"instanceName":"1"});
            var Q434;
            Q434=makeQuery(id+"F11.opPattern","COPY",BODY,{"derivedFrom":makeQuery(id+"F8.opPattern","COPY",BODY,{"derivedFrom":makeQuery(id+"F3.opPattern","COPY",BODY,{"derivedFrom":makeQuery(id+"F2.opPattern","COPY",BODY,{"derivedFrom":makeQuery(id+"F1.opRevolve","SWEPT_BODY",BODY,{"disambiguationData":[OSD([sQuery(id+"F0.wireOp",EDGE,"E1")])]}),"instanceName":"1"}),"instanceName":"1"}),"instanceName":"1"}),"instanceName":"1"});
            var Q435;
            Q435=makeQuery(id+"F11.opPattern","COPY",BODY,{"derivedFrom":makeQuery(id+"F8.opPattern","COPY",BODY,{"derivedFrom":makeQuery(id+"F4.opPattern","COPY",BODY,{"derivedFrom":makeQuery(id+"F1.opRevolve","SWEPT_BODY",BODY,{"disambiguationData":[OSD([sQuery(id+"F0.wireOp",EDGE,"E1")])]}),"instanceName":"1"}),"instanceName":"1"}),"instanceName":"1"});
            var Q436;
            Q436=makeQuery(id+"F11.opPattern","COPY",BODY,{"derivedFrom":makeQuery(id+"F8.opPattern","COPY",BODY,{"derivedFrom":makeQuery(id+"F4.opPattern","COPY",BODY,{"derivedFrom":makeQuery(id+"F2.opPattern","COPY",BODY,{"derivedFrom":makeQuery(id+"F1.opRevolve","SWEPT_BODY",BODY,{"disambiguationData":[OSD([sQuery(id+"F0.wireOp",EDGE,"E1")])]}),"instanceName":"1"}),"instanceName":"1"}),"instanceName":"1"}),"instanceName":"1"});
            var Q437;
            Q437=makeQuery(id+"F11.opPattern","COPY",BODY,{"derivedFrom":makeQuery(id+"F8.opPattern","COPY",BODY,{"derivedFrom":makeQuery(id+"F4.opPattern","COPY",BODY,{"derivedFrom":makeQuery(id+"F3.opPattern","COPY",BODY,{"derivedFrom":makeQuery(id+"F2.opPattern","COPY",BODY,{"derivedFrom":makeQuery(id+"F1.opRevolve","SWEPT_BODY",BODY,{"disambiguationData":[OSD([sQuery(id+"F0.wireOp",EDGE,"E1")])]}),"instanceName":"1"}),"instanceName":"1"}),"instanceName":"1"}),"instanceName":"1"}),"instanceName":"1"});
            var Q438;
            Q438=makeQuery(id+"F11.opPattern","COPY",BODY,{"derivedFrom":makeQuery(id+"F8.opPattern","COPY",BODY,{"derivedFrom":makeQuery(id+"F5.opPattern","COPY",BODY,{"derivedFrom":makeQuery(id+"F1.opRevolve","SWEPT_BODY",BODY,{"disambiguationData":[OSD([sQuery(id+"F0.wireOp",EDGE,"E1")])]}),"instanceName":"1"}),"instanceName":"1"}),"instanceName":"1"});
            var Q439;
            Q439=makeQuery(id+"F11.opPattern","COPY",BODY,{"derivedFrom":makeQuery(id+"F8.opPattern","COPY",BODY,{"derivedFrom":makeQuery(id+"F5.opPattern","COPY",BODY,{"derivedFrom":makeQuery(id+"F2.opPattern","COPY",BODY,{"derivedFrom":makeQuery(id+"F1.opRevolve","SWEPT_BODY",BODY,{"disambiguationData":[OSD([sQuery(id+"F0.wireOp",EDGE,"E1")])]}),"instanceName":"1"}),"instanceName":"1"}),"instanceName":"1"}),"instanceName":"1"});
            var Q440;
            Q440=makeQuery(id+"F11.opPattern","COPY",BODY,{"derivedFrom":makeQuery(id+"F8.opPattern","COPY",BODY,{"derivedFrom":makeQuery(id+"F5.opPattern","COPY",BODY,{"derivedFrom":makeQuery(id+"F3.opPattern","COPY",BODY,{"derivedFrom":makeQuery(id+"F2.opPattern","COPY",BODY,{"derivedFrom":makeQuery(id+"F1.opRevolve","SWEPT_BODY",BODY,{"disambiguationData":[OSD([sQuery(id+"F0.wireOp",EDGE,"E1")])]}),"instanceName":"1"}),"instanceName":"1"}),"instanceName":"1"}),"instanceName":"1"}),"instanceName":"1"});
            var Q441;
            Q441=makeQuery(id+"F11.opPattern","COPY",BODY,{"derivedFrom":makeQuery(id+"F8.opPattern","COPY",BODY,{"derivedFrom":makeQuery(id+"F5.opPattern","COPY",BODY,{"derivedFrom":makeQuery(id+"F4.opPattern","COPY",BODY,{"derivedFrom":makeQuery(id+"F1.opRevolve","SWEPT_BODY",BODY,{"disambiguationData":[OSD([sQuery(id+"F0.wireOp",EDGE,"E1")])]}),"instanceName":"1"}),"instanceName":"1"}),"instanceName":"1"}),"instanceName":"1"});
            var Q442;
            Q442=makeQuery(id+"F11.opPattern","COPY",BODY,{"derivedFrom":makeQuery(id+"F8.opPattern","COPY",BODY,{"derivedFrom":makeQuery(id+"F5.opPattern","COPY",BODY,{"derivedFrom":makeQuery(id+"F4.opPattern","COPY",BODY,{"derivedFrom":makeQuery(id+"F2.opPattern","COPY",BODY,{"derivedFrom":makeQuery(id+"F1.opRevolve","SWEPT_BODY",BODY,{"disambiguationData":[OSD([sQuery(id+"F0.wireOp",EDGE,"E1")])]}),"instanceName":"1"}),"instanceName":"1"}),"instanceName":"1"}),"instanceName":"1"}),"instanceName":"1"});
            var Q443;
            Q443=makeQuery(id+"F11.opPattern","COPY",BODY,{"derivedFrom":makeQuery(id+"F8.opPattern","COPY",BODY,{"derivedFrom":makeQuery(id+"F5.opPattern","COPY",BODY,{"derivedFrom":makeQuery(id+"F4.opPattern","COPY",BODY,{"derivedFrom":makeQuery(id+"F3.opPattern","COPY",BODY,{"derivedFrom":makeQuery(id+"F2.opPattern","COPY",BODY,{"derivedFrom":makeQuery(id+"F1.opRevolve","SWEPT_BODY",BODY,{"disambiguationData":[OSD([sQuery(id+"F0.wireOp",EDGE,"E1")])]}),"instanceName":"1"}),"instanceName":"1"}),"instanceName":"1"}),"instanceName":"1"}),"instanceName":"1"}),"instanceName":"1"});
            var Q444;
            Q444=makeQuery(id+"F11.opPattern","COPY",BODY,{"derivedFrom":makeQuery(id+"F8.opPattern","COPY",BODY,{"derivedFrom":makeQuery(id+"F6.opPattern","COPY",BODY,{"derivedFrom":makeQuery(id+"F1.opRevolve","SWEPT_BODY",BODY,{"disambiguationData":[OSD([sQuery(id+"F0.wireOp",EDGE,"E1")])]}),"instanceName":"1"}),"instanceName":"1"}),"instanceName":"1"});
            var Q445;
            Q445=makeQuery(id+"F11.opPattern","COPY",BODY,{"derivedFrom":makeQuery(id+"F8.opPattern","COPY",BODY,{"derivedFrom":makeQuery(id+"F6.opPattern","COPY",BODY,{"derivedFrom":makeQuery(id+"F2.opPattern","COPY",BODY,{"derivedFrom":makeQuery(id+"F1.opRevolve","SWEPT_BODY",BODY,{"disambiguationData":[OSD([sQuery(id+"F0.wireOp",EDGE,"E1")])]}),"instanceName":"1"}),"instanceName":"1"}),"instanceName":"1"}),"instanceName":"1"});
            var Q446;
            Q446=makeQuery(id+"F11.opPattern","COPY",BODY,{"derivedFrom":makeQuery(id+"F8.opPattern","COPY",BODY,{"derivedFrom":makeQuery(id+"F6.opPattern","COPY",BODY,{"derivedFrom":makeQuery(id+"F3.opPattern","COPY",BODY,{"derivedFrom":makeQuery(id+"F2.opPattern","COPY",BODY,{"derivedFrom":makeQuery(id+"F1.opRevolve","SWEPT_BODY",BODY,{"disambiguationData":[OSD([sQuery(id+"F0.wireOp",EDGE,"E1")])]}),"instanceName":"1"}),"instanceName":"1"}),"instanceName":"1"}),"instanceName":"1"}),"instanceName":"1"});
            var Q447;
            Q447=makeQuery(id+"F11.opPattern","COPY",BODY,{"derivedFrom":makeQuery(id+"F8.opPattern","COPY",BODY,{"derivedFrom":makeQuery(id+"F6.opPattern","COPY",BODY,{"derivedFrom":makeQuery(id+"F4.opPattern","COPY",BODY,{"derivedFrom":makeQuery(id+"F1.opRevolve","SWEPT_BODY",BODY,{"disambiguationData":[OSD([sQuery(id+"F0.wireOp",EDGE,"E1")])]}),"instanceName":"1"}),"instanceName":"1"}),"instanceName":"1"}),"instanceName":"1"});
            var Q448;
            Q448=makeQuery(id+"F11.opPattern","COPY",BODY,{"derivedFrom":makeQuery(id+"F8.opPattern","COPY",BODY,{"derivedFrom":makeQuery(id+"F6.opPattern","COPY",BODY,{"derivedFrom":makeQuery(id+"F4.opPattern","COPY",BODY,{"derivedFrom":makeQuery(id+"F2.opPattern","COPY",BODY,{"derivedFrom":makeQuery(id+"F1.opRevolve","SWEPT_BODY",BODY,{"disambiguationData":[OSD([sQuery(id+"F0.wireOp",EDGE,"E1")])]}),"instanceName":"1"}),"instanceName":"1"}),"instanceName":"1"}),"instanceName":"1"}),"instanceName":"1"});
            var Q449;
            Q449=makeQuery(id+"F11.opPattern","COPY",BODY,{"derivedFrom":makeQuery(id+"F8.opPattern","COPY",BODY,{"derivedFrom":makeQuery(id+"F6.opPattern","COPY",BODY,{"derivedFrom":makeQuery(id+"F4.opPattern","COPY",BODY,{"derivedFrom":makeQuery(id+"F3.opPattern","COPY",BODY,{"derivedFrom":makeQuery(id+"F2.opPattern","COPY",BODY,{"derivedFrom":makeQuery(id+"F1.opRevolve","SWEPT_BODY",BODY,{"disambiguationData":[OSD([sQuery(id+"F0.wireOp",EDGE,"E1")])]}),"instanceName":"1"}),"instanceName":"1"}),"instanceName":"1"}),"instanceName":"1"}),"instanceName":"1"}),"instanceName":"1"});
            var Q450;
            Q450=makeQuery(id+"F11.opPattern","COPY",BODY,{"derivedFrom":makeQuery(id+"F8.opPattern","COPY",BODY,{"derivedFrom":makeQuery(id+"F6.opPattern","COPY",BODY,{"derivedFrom":makeQuery(id+"F5.opPattern","COPY",BODY,{"derivedFrom":makeQuery(id+"F1.opRevolve","SWEPT_BODY",BODY,{"disambiguationData":[OSD([sQuery(id+"F0.wireOp",EDGE,"E1")])]}),"instanceName":"1"}),"instanceName":"1"}),"instanceName":"1"}),"instanceName":"1"});
            var Q451;
            Q451=makeQuery(id+"F11.opPattern","COPY",BODY,{"derivedFrom":makeQuery(id+"F8.opPattern","COPY",BODY,{"derivedFrom":makeQuery(id+"F6.opPattern","COPY",BODY,{"derivedFrom":makeQuery(id+"F5.opPattern","COPY",BODY,{"derivedFrom":makeQuery(id+"F2.opPattern","COPY",BODY,{"derivedFrom":makeQuery(id+"F1.opRevolve","SWEPT_BODY",BODY,{"disambiguationData":[OSD([sQuery(id+"F0.wireOp",EDGE,"E1")])]}),"instanceName":"1"}),"instanceName":"1"}),"instanceName":"1"}),"instanceName":"1"}),"instanceName":"1"});
            var Q452;
            Q452=makeQuery(id+"F11.opPattern","COPY",BODY,{"derivedFrom":makeQuery(id+"F8.opPattern","COPY",BODY,{"derivedFrom":makeQuery(id+"F6.opPattern","COPY",BODY,{"derivedFrom":makeQuery(id+"F5.opPattern","COPY",BODY,{"derivedFrom":makeQuery(id+"F3.opPattern","COPY",BODY,{"derivedFrom":makeQuery(id+"F2.opPattern","COPY",BODY,{"derivedFrom":makeQuery(id+"F1.opRevolve","SWEPT_BODY",BODY,{"disambiguationData":[OSD([sQuery(id+"F0.wireOp",EDGE,"E1")])]}),"instanceName":"1"}),"instanceName":"1"}),"instanceName":"1"}),"instanceName":"1"}),"instanceName":"1"}),"instanceName":"1"});
            var Q453;
            Q453=makeQuery(id+"F11.opPattern","COPY",BODY,{"derivedFrom":makeQuery(id+"F8.opPattern","COPY",BODY,{"derivedFrom":makeQuery(id+"F6.opPattern","COPY",BODY,{"derivedFrom":makeQuery(id+"F5.opPattern","COPY",BODY,{"derivedFrom":makeQuery(id+"F4.opPattern","COPY",BODY,{"derivedFrom":makeQuery(id+"F1.opRevolve","SWEPT_BODY",BODY,{"disambiguationData":[OSD([sQuery(id+"F0.wireOp",EDGE,"E1")])]}),"instanceName":"1"}),"instanceName":"1"}),"instanceName":"1"}),"instanceName":"1"}),"instanceName":"1"});
            var Q454;
            Q454=makeQuery(id+"F11.opPattern","COPY",BODY,{"derivedFrom":makeQuery(id+"F8.opPattern","COPY",BODY,{"derivedFrom":makeQuery(id+"F6.opPattern","COPY",BODY,{"derivedFrom":makeQuery(id+"F5.opPattern","COPY",BODY,{"derivedFrom":makeQuery(id+"F4.opPattern","COPY",BODY,{"derivedFrom":makeQuery(id+"F2.opPattern","COPY",BODY,{"derivedFrom":makeQuery(id+"F1.opRevolve","SWEPT_BODY",BODY,{"disambiguationData":[OSD([sQuery(id+"F0.wireOp",EDGE,"E1")])]}),"instanceName":"1"}),"instanceName":"1"}),"instanceName":"1"}),"instanceName":"1"}),"instanceName":"1"}),"instanceName":"1"});
            var Q455;
            Q455=makeQuery(id+"F11.opPattern","COPY",BODY,{"derivedFrom":makeQuery(id+"F8.opPattern","COPY",BODY,{"derivedFrom":makeQuery(id+"F6.opPattern","COPY",BODY,{"derivedFrom":makeQuery(id+"F5.opPattern","COPY",BODY,{"derivedFrom":makeQuery(id+"F4.opPattern","COPY",BODY,{"derivedFrom":makeQuery(id+"F3.opPattern","COPY",BODY,{"derivedFrom":makeQuery(id+"F2.opPattern","COPY",BODY,{"derivedFrom":makeQuery(id+"F1.opRevolve","SWEPT_BODY",BODY,{"disambiguationData":[OSD([sQuery(id+"F0.wireOp",EDGE,"E1")])]}),"instanceName":"1"}),"instanceName":"1"}),"instanceName":"1"}),"instanceName":"1"}),"instanceName":"1"}),"instanceName":"1"}),"instanceName":"1"});
            var Q456;
            Q456=makeQuery(id+"F11.opPattern","COPY",BODY,{"derivedFrom":makeQuery(id+"F8.opPattern","COPY",BODY,{"derivedFrom":makeQuery(id+"F7.opPattern","COPY",BODY,{"derivedFrom":makeQuery(id+"F1.opRevolve","SWEPT_BODY",BODY,{"disambiguationData":[OSD([sQuery(id+"F0.wireOp",EDGE,"E1")])]}),"instanceName":"1"}),"instanceName":"1"}),"instanceName":"1"});
            var Q457;
            Q457=makeQuery(id+"F11.opPattern","COPY",BODY,{"derivedFrom":makeQuery(id+"F8.opPattern","COPY",BODY,{"derivedFrom":makeQuery(id+"F7.opPattern","COPY",BODY,{"derivedFrom":makeQuery(id+"F2.opPattern","COPY",BODY,{"derivedFrom":makeQuery(id+"F1.opRevolve","SWEPT_BODY",BODY,{"disambiguationData":[OSD([sQuery(id+"F0.wireOp",EDGE,"E1")])]}),"instanceName":"1"}),"instanceName":"1"}),"instanceName":"1"}),"instanceName":"1"});
            var Q458;
            Q458=makeQuery(id+"F11.opPattern","COPY",BODY,{"derivedFrom":makeQuery(id+"F8.opPattern","COPY",BODY,{"derivedFrom":makeQuery(id+"F7.opPattern","COPY",BODY,{"derivedFrom":makeQuery(id+"F3.opPattern","COPY",BODY,{"derivedFrom":makeQuery(id+"F2.opPattern","COPY",BODY,{"derivedFrom":makeQuery(id+"F1.opRevolve","SWEPT_BODY",BODY,{"disambiguationData":[OSD([sQuery(id+"F0.wireOp",EDGE,"E1")])]}),"instanceName":"1"}),"instanceName":"1"}),"instanceName":"1"}),"instanceName":"1"}),"instanceName":"1"});
            var Q459;
            Q459=makeQuery(id+"F11.opPattern","COPY",BODY,{"derivedFrom":makeQuery(id+"F8.opPattern","COPY",BODY,{"derivedFrom":makeQuery(id+"F7.opPattern","COPY",BODY,{"derivedFrom":makeQuery(id+"F4.opPattern","COPY",BODY,{"derivedFrom":makeQuery(id+"F1.opRevolve","SWEPT_BODY",BODY,{"disambiguationData":[OSD([sQuery(id+"F0.wireOp",EDGE,"E1")])]}),"instanceName":"1"}),"instanceName":"1"}),"instanceName":"1"}),"instanceName":"1"});
            var Q460;
            Q460=makeQuery(id+"F11.opPattern","COPY",BODY,{"derivedFrom":makeQuery(id+"F8.opPattern","COPY",BODY,{"derivedFrom":makeQuery(id+"F7.opPattern","COPY",BODY,{"derivedFrom":makeQuery(id+"F4.opPattern","COPY",BODY,{"derivedFrom":makeQuery(id+"F2.opPattern","COPY",BODY,{"derivedFrom":makeQuery(id+"F1.opRevolve","SWEPT_BODY",BODY,{"disambiguationData":[OSD([sQuery(id+"F0.wireOp",EDGE,"E1")])]}),"instanceName":"1"}),"instanceName":"1"}),"instanceName":"1"}),"instanceName":"1"}),"instanceName":"1"});
            var Q461;
            Q461=makeQuery(id+"F11.opPattern","COPY",BODY,{"derivedFrom":makeQuery(id+"F8.opPattern","COPY",BODY,{"derivedFrom":makeQuery(id+"F7.opPattern","COPY",BODY,{"derivedFrom":makeQuery(id+"F4.opPattern","COPY",BODY,{"derivedFrom":makeQuery(id+"F3.opPattern","COPY",BODY,{"derivedFrom":makeQuery(id+"F2.opPattern","COPY",BODY,{"derivedFrom":makeQuery(id+"F1.opRevolve","SWEPT_BODY",BODY,{"disambiguationData":[OSD([sQuery(id+"F0.wireOp",EDGE,"E1")])]}),"instanceName":"1"}),"instanceName":"1"}),"instanceName":"1"}),"instanceName":"1"}),"instanceName":"1"}),"instanceName":"1"});
            var Q462;
            Q462=makeQuery(id+"F11.opPattern","COPY",BODY,{"derivedFrom":makeQuery(id+"F8.opPattern","COPY",BODY,{"derivedFrom":makeQuery(id+"F7.opPattern","COPY",BODY,{"derivedFrom":makeQuery(id+"F5.opPattern","COPY",BODY,{"derivedFrom":makeQuery(id+"F1.opRevolve","SWEPT_BODY",BODY,{"disambiguationData":[OSD([sQuery(id+"F0.wireOp",EDGE,"E1")])]}),"instanceName":"1"}),"instanceName":"1"}),"instanceName":"1"}),"instanceName":"1"});
            var Q463;
            Q463=makeQuery(id+"F11.opPattern","COPY",BODY,{"derivedFrom":makeQuery(id+"F8.opPattern","COPY",BODY,{"derivedFrom":makeQuery(id+"F7.opPattern","COPY",BODY,{"derivedFrom":makeQuery(id+"F5.opPattern","COPY",BODY,{"derivedFrom":makeQuery(id+"F2.opPattern","COPY",BODY,{"derivedFrom":makeQuery(id+"F1.opRevolve","SWEPT_BODY",BODY,{"disambiguationData":[OSD([sQuery(id+"F0.wireOp",EDGE,"E1")])]}),"instanceName":"1"}),"instanceName":"1"}),"instanceName":"1"}),"instanceName":"1"}),"instanceName":"1"});
            var Q464;
            Q464=makeQuery(id+"F11.opPattern","COPY",BODY,{"derivedFrom":makeQuery(id+"F8.opPattern","COPY",BODY,{"derivedFrom":makeQuery(id+"F7.opPattern","COPY",BODY,{"derivedFrom":makeQuery(id+"F5.opPattern","COPY",BODY,{"derivedFrom":makeQuery(id+"F3.opPattern","COPY",BODY,{"derivedFrom":makeQuery(id+"F2.opPattern","COPY",BODY,{"derivedFrom":makeQuery(id+"F1.opRevolve","SWEPT_BODY",BODY,{"disambiguationData":[OSD([sQuery(id+"F0.wireOp",EDGE,"E1")])]}),"instanceName":"1"}),"instanceName":"1"}),"instanceName":"1"}),"instanceName":"1"}),"instanceName":"1"}),"instanceName":"1"});
            var Q465;
            Q465=makeQuery(id+"F11.opPattern","COPY",BODY,{"derivedFrom":makeQuery(id+"F8.opPattern","COPY",BODY,{"derivedFrom":makeQuery(id+"F7.opPattern","COPY",BODY,{"derivedFrom":makeQuery(id+"F5.opPattern","COPY",BODY,{"derivedFrom":makeQuery(id+"F4.opPattern","COPY",BODY,{"derivedFrom":makeQuery(id+"F1.opRevolve","SWEPT_BODY",BODY,{"disambiguationData":[OSD([sQuery(id+"F0.wireOp",EDGE,"E1")])]}),"instanceName":"1"}),"instanceName":"1"}),"instanceName":"1"}),"instanceName":"1"}),"instanceName":"1"});
            var Q466;
            Q466=makeQuery(id+"F11.opPattern","COPY",BODY,{"derivedFrom":makeQuery(id+"F8.opPattern","COPY",BODY,{"derivedFrom":makeQuery(id+"F7.opPattern","COPY",BODY,{"derivedFrom":makeQuery(id+"F5.opPattern","COPY",BODY,{"derivedFrom":makeQuery(id+"F4.opPattern","COPY",BODY,{"derivedFrom":makeQuery(id+"F2.opPattern","COPY",BODY,{"derivedFrom":makeQuery(id+"F1.opRevolve","SWEPT_BODY",BODY,{"disambiguationData":[OSD([sQuery(id+"F0.wireOp",EDGE,"E1")])]}),"instanceName":"1"}),"instanceName":"1"}),"instanceName":"1"}),"instanceName":"1"}),"instanceName":"1"}),"instanceName":"1"});
            var Q467;
            Q467=makeQuery(id+"F11.opPattern","COPY",BODY,{"derivedFrom":makeQuery(id+"F8.opPattern","COPY",BODY,{"derivedFrom":makeQuery(id+"F7.opPattern","COPY",BODY,{"derivedFrom":makeQuery(id+"F5.opPattern","COPY",BODY,{"derivedFrom":makeQuery(id+"F4.opPattern","COPY",BODY,{"derivedFrom":makeQuery(id+"F3.opPattern","COPY",BODY,{"derivedFrom":makeQuery(id+"F2.opPattern","COPY",BODY,{"derivedFrom":makeQuery(id+"F1.opRevolve","SWEPT_BODY",BODY,{"disambiguationData":[OSD([sQuery(id+"F0.wireOp",EDGE,"E1")])]}),"instanceName":"1"}),"instanceName":"1"}),"instanceName":"1"}),"instanceName":"1"}),"instanceName":"1"}),"instanceName":"1"}),"instanceName":"1"});
            var Q468;
            Q468=makeQuery(id+"F11.opPattern","COPY",BODY,{"derivedFrom":makeQuery(id+"F8.opPattern","COPY",BODY,{"derivedFrom":makeQuery(id+"F7.opPattern","COPY",BODY,{"derivedFrom":makeQuery(id+"F6.opPattern","COPY",BODY,{"derivedFrom":makeQuery(id+"F1.opRevolve","SWEPT_BODY",BODY,{"disambiguationData":[OSD([sQuery(id+"F0.wireOp",EDGE,"E1")])]}),"instanceName":"1"}),"instanceName":"1"}),"instanceName":"1"}),"instanceName":"1"});
            var Q469;
            Q469=makeQuery(id+"F11.opPattern","COPY",BODY,{"derivedFrom":makeQuery(id+"F8.opPattern","COPY",BODY,{"derivedFrom":makeQuery(id+"F7.opPattern","COPY",BODY,{"derivedFrom":makeQuery(id+"F6.opPattern","COPY",BODY,{"derivedFrom":makeQuery(id+"F2.opPattern","COPY",BODY,{"derivedFrom":makeQuery(id+"F1.opRevolve","SWEPT_BODY",BODY,{"disambiguationData":[OSD([sQuery(id+"F0.wireOp",EDGE,"E1")])]}),"instanceName":"1"}),"instanceName":"1"}),"instanceName":"1"}),"instanceName":"1"}),"instanceName":"1"});
            var Q470;
            Q470=makeQuery(id+"F11.opPattern","COPY",BODY,{"derivedFrom":makeQuery(id+"F8.opPattern","COPY",BODY,{"derivedFrom":makeQuery(id+"F7.opPattern","COPY",BODY,{"derivedFrom":makeQuery(id+"F6.opPattern","COPY",BODY,{"derivedFrom":makeQuery(id+"F3.opPattern","COPY",BODY,{"derivedFrom":makeQuery(id+"F2.opPattern","COPY",BODY,{"derivedFrom":makeQuery(id+"F1.opRevolve","SWEPT_BODY",BODY,{"disambiguationData":[OSD([sQuery(id+"F0.wireOp",EDGE,"E1")])]}),"instanceName":"1"}),"instanceName":"1"}),"instanceName":"1"}),"instanceName":"1"}),"instanceName":"1"}),"instanceName":"1"});
            var Q471;
            Q471=makeQuery(id+"F11.opPattern","COPY",BODY,{"derivedFrom":makeQuery(id+"F8.opPattern","COPY",BODY,{"derivedFrom":makeQuery(id+"F7.opPattern","COPY",BODY,{"derivedFrom":makeQuery(id+"F6.opPattern","COPY",BODY,{"derivedFrom":makeQuery(id+"F4.opPattern","COPY",BODY,{"derivedFrom":makeQuery(id+"F1.opRevolve","SWEPT_BODY",BODY,{"disambiguationData":[OSD([sQuery(id+"F0.wireOp",EDGE,"E1")])]}),"instanceName":"1"}),"instanceName":"1"}),"instanceName":"1"}),"instanceName":"1"}),"instanceName":"1"});
            var Q472;
            Q472=makeQuery(id+"F11.opPattern","COPY",BODY,{"derivedFrom":makeQuery(id+"F8.opPattern","COPY",BODY,{"derivedFrom":makeQuery(id+"F7.opPattern","COPY",BODY,{"derivedFrom":makeQuery(id+"F6.opPattern","COPY",BODY,{"derivedFrom":makeQuery(id+"F4.opPattern","COPY",BODY,{"derivedFrom":makeQuery(id+"F2.opPattern","COPY",BODY,{"derivedFrom":makeQuery(id+"F1.opRevolve","SWEPT_BODY",BODY,{"disambiguationData":[OSD([sQuery(id+"F0.wireOp",EDGE,"E1")])]}),"instanceName":"1"}),"instanceName":"1"}),"instanceName":"1"}),"instanceName":"1"}),"instanceName":"1"}),"instanceName":"1"});
            var Q473;
            Q473=makeQuery(id+"F11.opPattern","COPY",BODY,{"derivedFrom":makeQuery(id+"F8.opPattern","COPY",BODY,{"derivedFrom":makeQuery(id+"F7.opPattern","COPY",BODY,{"derivedFrom":makeQuery(id+"F6.opPattern","COPY",BODY,{"derivedFrom":makeQuery(id+"F4.opPattern","COPY",BODY,{"derivedFrom":makeQuery(id+"F3.opPattern","COPY",BODY,{"derivedFrom":makeQuery(id+"F2.opPattern","COPY",BODY,{"derivedFrom":makeQuery(id+"F1.opRevolve","SWEPT_BODY",BODY,{"disambiguationData":[OSD([sQuery(id+"F0.wireOp",EDGE,"E1")])]}),"instanceName":"1"}),"instanceName":"1"}),"instanceName":"1"}),"instanceName":"1"}),"instanceName":"1"}),"instanceName":"1"}),"instanceName":"1"});
            var Q474;
            Q474=makeQuery(id+"F11.opPattern","COPY",BODY,{"derivedFrom":makeQuery(id+"F8.opPattern","COPY",BODY,{"derivedFrom":makeQuery(id+"F7.opPattern","COPY",BODY,{"derivedFrom":makeQuery(id+"F6.opPattern","COPY",BODY,{"derivedFrom":makeQuery(id+"F5.opPattern","COPY",BODY,{"derivedFrom":makeQuery(id+"F1.opRevolve","SWEPT_BODY",BODY,{"disambiguationData":[OSD([sQuery(id+"F0.wireOp",EDGE,"E1")])]}),"instanceName":"1"}),"instanceName":"1"}),"instanceName":"1"}),"instanceName":"1"}),"instanceName":"1"});
            var Q475;
            Q475=makeQuery(id+"F11.opPattern","COPY",BODY,{"derivedFrom":makeQuery(id+"F8.opPattern","COPY",BODY,{"derivedFrom":makeQuery(id+"F7.opPattern","COPY",BODY,{"derivedFrom":makeQuery(id+"F6.opPattern","COPY",BODY,{"derivedFrom":makeQuery(id+"F5.opPattern","COPY",BODY,{"derivedFrom":makeQuery(id+"F2.opPattern","COPY",BODY,{"derivedFrom":makeQuery(id+"F1.opRevolve","SWEPT_BODY",BODY,{"disambiguationData":[OSD([sQuery(id+"F0.wireOp",EDGE,"E1")])]}),"instanceName":"1"}),"instanceName":"1"}),"instanceName":"1"}),"instanceName":"1"}),"instanceName":"1"}),"instanceName":"1"});
            var Q476;
            Q476=makeQuery(id+"F11.opPattern","COPY",BODY,{"derivedFrom":makeQuery(id+"F8.opPattern","COPY",BODY,{"derivedFrom":makeQuery(id+"F7.opPattern","COPY",BODY,{"derivedFrom":makeQuery(id+"F6.opPattern","COPY",BODY,{"derivedFrom":makeQuery(id+"F5.opPattern","COPY",BODY,{"derivedFrom":makeQuery(id+"F3.opPattern","COPY",BODY,{"derivedFrom":makeQuery(id+"F2.opPattern","COPY",BODY,{"derivedFrom":makeQuery(id+"F1.opRevolve","SWEPT_BODY",BODY,{"disambiguationData":[OSD([sQuery(id+"F0.wireOp",EDGE,"E1")])]}),"instanceName":"1"}),"instanceName":"1"}),"instanceName":"1"}),"instanceName":"1"}),"instanceName":"1"}),"instanceName":"1"}),"instanceName":"1"});
            var Q477;
            Q477=makeQuery(id+"F11.opPattern","COPY",BODY,{"derivedFrom":makeQuery(id+"F8.opPattern","COPY",BODY,{"derivedFrom":makeQuery(id+"F7.opPattern","COPY",BODY,{"derivedFrom":makeQuery(id+"F6.opPattern","COPY",BODY,{"derivedFrom":makeQuery(id+"F5.opPattern","COPY",BODY,{"derivedFrom":makeQuery(id+"F4.opPattern","COPY",BODY,{"derivedFrom":makeQuery(id+"F1.opRevolve","SWEPT_BODY",BODY,{"disambiguationData":[OSD([sQuery(id+"F0.wireOp",EDGE,"E1")])]}),"instanceName":"1"}),"instanceName":"1"}),"instanceName":"1"}),"instanceName":"1"}),"instanceName":"1"}),"instanceName":"1"});
            var Q478;
            Q478=makeQuery(id+"F11.opPattern","COPY",BODY,{"derivedFrom":makeQuery(id+"F8.opPattern","COPY",BODY,{"derivedFrom":makeQuery(id+"F7.opPattern","COPY",BODY,{"derivedFrom":makeQuery(id+"F6.opPattern","COPY",BODY,{"derivedFrom":makeQuery(id+"F5.opPattern","COPY",BODY,{"derivedFrom":makeQuery(id+"F4.opPattern","COPY",BODY,{"derivedFrom":makeQuery(id+"F2.opPattern","COPY",BODY,{"derivedFrom":makeQuery(id+"F1.opRevolve","SWEPT_BODY",BODY,{"disambiguationData":[OSD([sQuery(id+"F0.wireOp",EDGE,"E1")])]}),"instanceName":"1"}),"instanceName":"1"}),"instanceName":"1"}),"instanceName":"1"}),"instanceName":"1"}),"instanceName":"1"}),"instanceName":"1"});
            var Q479;
            Q479=makeQuery(id+"F11.opPattern","COPY",BODY,{"derivedFrom":makeQuery(id+"F8.opPattern","COPY",BODY,{"derivedFrom":makeQuery(id+"F7.opPattern","COPY",BODY,{"derivedFrom":makeQuery(id+"F6.opPattern","COPY",BODY,{"derivedFrom":makeQuery(id+"F5.opPattern","COPY",BODY,{"derivedFrom":makeQuery(id+"F4.opPattern","COPY",BODY,{"derivedFrom":makeQuery(id+"F3.opPattern","COPY",BODY,{"derivedFrom":makeQuery(id+"F2.opPattern","COPY",BODY,{"derivedFrom":makeQuery(id+"F1.opRevolve","SWEPT_BODY",BODY,{"disambiguationData":[OSD([sQuery(id+"F0.wireOp",EDGE,"E1")])]}),"instanceName":"1"}),"instanceName":"1"}),"instanceName":"1"}),"instanceName":"1"}),"instanceName":"1"}),"instanceName":"1"}),"instanceName":"1"}),"instanceName":"1"});
            var Q480;
            Q480=makeQuery(id+"F11.opPattern","COPY",BODY,{"derivedFrom":makeQuery(id+"F9.opPattern","COPY",BODY,{"derivedFrom":makeQuery(id+"F1.opRevolve","SWEPT_BODY",BODY,{"disambiguationData":[OSD([sQuery(id+"F0.wireOp",EDGE,"E1")])]}),"instanceName":"1"}),"instanceName":"1"});
            var Q481;
            Q481=makeQuery(id+"F11.opPattern","COPY",BODY,{"derivedFrom":makeQuery(id+"F9.opPattern","COPY",BODY,{"derivedFrom":makeQuery(id+"F2.opPattern","COPY",BODY,{"derivedFrom":makeQuery(id+"F1.opRevolve","SWEPT_BODY",BODY,{"disambiguationData":[OSD([sQuery(id+"F0.wireOp",EDGE,"E1")])]}),"instanceName":"1"}),"instanceName":"1"}),"instanceName":"1"});
            var Q482;
            Q482=makeQuery(id+"F11.opPattern","COPY",BODY,{"derivedFrom":makeQuery(id+"F9.opPattern","COPY",BODY,{"derivedFrom":makeQuery(id+"F3.opPattern","COPY",BODY,{"derivedFrom":makeQuery(id+"F2.opPattern","COPY",BODY,{"derivedFrom":makeQuery(id+"F1.opRevolve","SWEPT_BODY",BODY,{"disambiguationData":[OSD([sQuery(id+"F0.wireOp",EDGE,"E1")])]}),"instanceName":"1"}),"instanceName":"1"}),"instanceName":"1"}),"instanceName":"1"});
            var Q483;
            Q483=makeQuery(id+"F11.opPattern","COPY",BODY,{"derivedFrom":makeQuery(id+"F9.opPattern","COPY",BODY,{"derivedFrom":makeQuery(id+"F4.opPattern","COPY",BODY,{"derivedFrom":makeQuery(id+"F1.opRevolve","SWEPT_BODY",BODY,{"disambiguationData":[OSD([sQuery(id+"F0.wireOp",EDGE,"E1")])]}),"instanceName":"1"}),"instanceName":"1"}),"instanceName":"1"});
            var Q484;
            Q484=makeQuery(id+"F11.opPattern","COPY",BODY,{"derivedFrom":makeQuery(id+"F9.opPattern","COPY",BODY,{"derivedFrom":makeQuery(id+"F4.opPattern","COPY",BODY,{"derivedFrom":makeQuery(id+"F2.opPattern","COPY",BODY,{"derivedFrom":makeQuery(id+"F1.opRevolve","SWEPT_BODY",BODY,{"disambiguationData":[OSD([sQuery(id+"F0.wireOp",EDGE,"E1")])]}),"instanceName":"1"}),"instanceName":"1"}),"instanceName":"1"}),"instanceName":"1"});
            var Q485;
            Q485=makeQuery(id+"F11.opPattern","COPY",BODY,{"derivedFrom":makeQuery(id+"F9.opPattern","COPY",BODY,{"derivedFrom":makeQuery(id+"F4.opPattern","COPY",BODY,{"derivedFrom":makeQuery(id+"F3.opPattern","COPY",BODY,{"derivedFrom":makeQuery(id+"F2.opPattern","COPY",BODY,{"derivedFrom":makeQuery(id+"F1.opRevolve","SWEPT_BODY",BODY,{"disambiguationData":[OSD([sQuery(id+"F0.wireOp",EDGE,"E1")])]}),"instanceName":"1"}),"instanceName":"1"}),"instanceName":"1"}),"instanceName":"1"}),"instanceName":"1"});
            var Q486;
            Q486=makeQuery(id+"F11.opPattern","COPY",BODY,{"derivedFrom":makeQuery(id+"F9.opPattern","COPY",BODY,{"derivedFrom":makeQuery(id+"F5.opPattern","COPY",BODY,{"derivedFrom":makeQuery(id+"F1.opRevolve","SWEPT_BODY",BODY,{"disambiguationData":[OSD([sQuery(id+"F0.wireOp",EDGE,"E1")])]}),"instanceName":"1"}),"instanceName":"1"}),"instanceName":"1"});
            var Q487;
            Q487=makeQuery(id+"F11.opPattern","COPY",BODY,{"derivedFrom":makeQuery(id+"F9.opPattern","COPY",BODY,{"derivedFrom":makeQuery(id+"F5.opPattern","COPY",BODY,{"derivedFrom":makeQuery(id+"F2.opPattern","COPY",BODY,{"derivedFrom":makeQuery(id+"F1.opRevolve","SWEPT_BODY",BODY,{"disambiguationData":[OSD([sQuery(id+"F0.wireOp",EDGE,"E1")])]}),"instanceName":"1"}),"instanceName":"1"}),"instanceName":"1"}),"instanceName":"1"});
            var Q488;
            Q488=makeQuery(id+"F11.opPattern","COPY",BODY,{"derivedFrom":makeQuery(id+"F9.opPattern","COPY",BODY,{"derivedFrom":makeQuery(id+"F5.opPattern","COPY",BODY,{"derivedFrom":makeQuery(id+"F3.opPattern","COPY",BODY,{"derivedFrom":makeQuery(id+"F2.opPattern","COPY",BODY,{"derivedFrom":makeQuery(id+"F1.opRevolve","SWEPT_BODY",BODY,{"disambiguationData":[OSD([sQuery(id+"F0.wireOp",EDGE,"E1")])]}),"instanceName":"1"}),"instanceName":"1"}),"instanceName":"1"}),"instanceName":"1"}),"instanceName":"1"});
            var Q489;
            Q489=makeQuery(id+"F11.opPattern","COPY",BODY,{"derivedFrom":makeQuery(id+"F9.opPattern","COPY",BODY,{"derivedFrom":makeQuery(id+"F5.opPattern","COPY",BODY,{"derivedFrom":makeQuery(id+"F4.opPattern","COPY",BODY,{"derivedFrom":makeQuery(id+"F1.opRevolve","SWEPT_BODY",BODY,{"disambiguationData":[OSD([sQuery(id+"F0.wireOp",EDGE,"E1")])]}),"instanceName":"1"}),"instanceName":"1"}),"instanceName":"1"}),"instanceName":"1"});
            var Q490;
            Q490=makeQuery(id+"F11.opPattern","COPY",BODY,{"derivedFrom":makeQuery(id+"F9.opPattern","COPY",BODY,{"derivedFrom":makeQuery(id+"F5.opPattern","COPY",BODY,{"derivedFrom":makeQuery(id+"F4.opPattern","COPY",BODY,{"derivedFrom":makeQuery(id+"F2.opPattern","COPY",BODY,{"derivedFrom":makeQuery(id+"F1.opRevolve","SWEPT_BODY",BODY,{"disambiguationData":[OSD([sQuery(id+"F0.wireOp",EDGE,"E1")])]}),"instanceName":"1"}),"instanceName":"1"}),"instanceName":"1"}),"instanceName":"1"}),"instanceName":"1"});
            var Q491;
            Q491=makeQuery(id+"F11.opPattern","COPY",BODY,{"derivedFrom":makeQuery(id+"F9.opPattern","COPY",BODY,{"derivedFrom":makeQuery(id+"F5.opPattern","COPY",BODY,{"derivedFrom":makeQuery(id+"F4.opPattern","COPY",BODY,{"derivedFrom":makeQuery(id+"F3.opPattern","COPY",BODY,{"derivedFrom":makeQuery(id+"F2.opPattern","COPY",BODY,{"derivedFrom":makeQuery(id+"F1.opRevolve","SWEPT_BODY",BODY,{"disambiguationData":[OSD([sQuery(id+"F0.wireOp",EDGE,"E1")])]}),"instanceName":"1"}),"instanceName":"1"}),"instanceName":"1"}),"instanceName":"1"}),"instanceName":"1"}),"instanceName":"1"});
            var Q492;
            Q492=makeQuery(id+"F11.opPattern","COPY",BODY,{"derivedFrom":makeQuery(id+"F9.opPattern","COPY",BODY,{"derivedFrom":makeQuery(id+"F6.opPattern","COPY",BODY,{"derivedFrom":makeQuery(id+"F1.opRevolve","SWEPT_BODY",BODY,{"disambiguationData":[OSD([sQuery(id+"F0.wireOp",EDGE,"E1")])]}),"instanceName":"1"}),"instanceName":"1"}),"instanceName":"1"});
            var Q493;
            Q493=makeQuery(id+"F11.opPattern","COPY",BODY,{"derivedFrom":makeQuery(id+"F9.opPattern","COPY",BODY,{"derivedFrom":makeQuery(id+"F6.opPattern","COPY",BODY,{"derivedFrom":makeQuery(id+"F2.opPattern","COPY",BODY,{"derivedFrom":makeQuery(id+"F1.opRevolve","SWEPT_BODY",BODY,{"disambiguationData":[OSD([sQuery(id+"F0.wireOp",EDGE,"E1")])]}),"instanceName":"1"}),"instanceName":"1"}),"instanceName":"1"}),"instanceName":"1"});
            var Q494;
            Q494=makeQuery(id+"F11.opPattern","COPY",BODY,{"derivedFrom":makeQuery(id+"F9.opPattern","COPY",BODY,{"derivedFrom":makeQuery(id+"F6.opPattern","COPY",BODY,{"derivedFrom":makeQuery(id+"F3.opPattern","COPY",BODY,{"derivedFrom":makeQuery(id+"F2.opPattern","COPY",BODY,{"derivedFrom":makeQuery(id+"F1.opRevolve","SWEPT_BODY",BODY,{"disambiguationData":[OSD([sQuery(id+"F0.wireOp",EDGE,"E1")])]}),"instanceName":"1"}),"instanceName":"1"}),"instanceName":"1"}),"instanceName":"1"}),"instanceName":"1"});
            var Q495;
            Q495=makeQuery(id+"F11.opPattern","COPY",BODY,{"derivedFrom":makeQuery(id+"F9.opPattern","COPY",BODY,{"derivedFrom":makeQuery(id+"F6.opPattern","COPY",BODY,{"derivedFrom":makeQuery(id+"F4.opPattern","COPY",BODY,{"derivedFrom":makeQuery(id+"F1.opRevolve","SWEPT_BODY",BODY,{"disambiguationData":[OSD([sQuery(id+"F0.wireOp",EDGE,"E1")])]}),"instanceName":"1"}),"instanceName":"1"}),"instanceName":"1"}),"instanceName":"1"});
            var Q496;
            Q496=makeQuery(id+"F11.opPattern","COPY",BODY,{"derivedFrom":makeQuery(id+"F9.opPattern","COPY",BODY,{"derivedFrom":makeQuery(id+"F6.opPattern","COPY",BODY,{"derivedFrom":makeQuery(id+"F4.opPattern","COPY",BODY,{"derivedFrom":makeQuery(id+"F2.opPattern","COPY",BODY,{"derivedFrom":makeQuery(id+"F1.opRevolve","SWEPT_BODY",BODY,{"disambiguationData":[OSD([sQuery(id+"F0.wireOp",EDGE,"E1")])]}),"instanceName":"1"}),"instanceName":"1"}),"instanceName":"1"}),"instanceName":"1"}),"instanceName":"1"});
            var Q497;
            Q497=makeQuery(id+"F11.opPattern","COPY",BODY,{"derivedFrom":makeQuery(id+"F9.opPattern","COPY",BODY,{"derivedFrom":makeQuery(id+"F6.opPattern","COPY",BODY,{"derivedFrom":makeQuery(id+"F4.opPattern","COPY",BODY,{"derivedFrom":makeQuery(id+"F3.opPattern","COPY",BODY,{"derivedFrom":makeQuery(id+"F2.opPattern","COPY",BODY,{"derivedFrom":makeQuery(id+"F1.opRevolve","SWEPT_BODY",BODY,{"disambiguationData":[OSD([sQuery(id+"F0.wireOp",EDGE,"E1")])]}),"instanceName":"1"}),"instanceName":"1"}),"instanceName":"1"}),"instanceName":"1"}),"instanceName":"1"}),"instanceName":"1"});
            var Q498;
            Q498=makeQuery(id+"F11.opPattern","COPY",BODY,{"derivedFrom":makeQuery(id+"F9.opPattern","COPY",BODY,{"derivedFrom":makeQuery(id+"F6.opPattern","COPY",BODY,{"derivedFrom":makeQuery(id+"F5.opPattern","COPY",BODY,{"derivedFrom":makeQuery(id+"F1.opRevolve","SWEPT_BODY",BODY,{"disambiguationData":[OSD([sQuery(id+"F0.wireOp",EDGE,"E1")])]}),"instanceName":"1"}),"instanceName":"1"}),"instanceName":"1"}),"instanceName":"1"});
            var Q499;
            Q499=makeQuery(id+"F11.opPattern","COPY",BODY,{"derivedFrom":makeQuery(id+"F9.opPattern","COPY",BODY,{"derivedFrom":makeQuery(id+"F6.opPattern","COPY",BODY,{"derivedFrom":makeQuery(id+"F5.opPattern","COPY",BODY,{"derivedFrom":makeQuery(id+"F2.opPattern","COPY",BODY,{"derivedFrom":makeQuery(id+"F1.opRevolve","SWEPT_BODY",BODY,{"disambiguationData":[OSD([sQuery(id+"F0.wireOp",EDGE,"E1")])]}),"instanceName":"1"}),"instanceName":"1"}),"instanceName":"1"}),"instanceName":"1"}),"instanceName":"1"});
            var Q500;
            Q500=makeQuery(id+"F11.opPattern","COPY",BODY,{"derivedFrom":makeQuery(id+"F9.opPattern","COPY",BODY,{"derivedFrom":makeQuery(id+"F6.opPattern","COPY",BODY,{"derivedFrom":makeQuery(id+"F5.opPattern","COPY",BODY,{"derivedFrom":makeQuery(id+"F3.opPattern","COPY",BODY,{"derivedFrom":makeQuery(id+"F2.opPattern","COPY",BODY,{"derivedFrom":makeQuery(id+"F1.opRevolve","SWEPT_BODY",BODY,{"disambiguationData":[OSD([sQuery(id+"F0.wireOp",EDGE,"E1")])]}),"instanceName":"1"}),"instanceName":"1"}),"instanceName":"1"}),"instanceName":"1"}),"instanceName":"1"}),"instanceName":"1"});
            var Q501;
            Q501=makeQuery(id+"F11.opPattern","COPY",BODY,{"derivedFrom":makeQuery(id+"F9.opPattern","COPY",BODY,{"derivedFrom":makeQuery(id+"F6.opPattern","COPY",BODY,{"derivedFrom":makeQuery(id+"F5.opPattern","COPY",BODY,{"derivedFrom":makeQuery(id+"F4.opPattern","COPY",BODY,{"derivedFrom":makeQuery(id+"F1.opRevolve","SWEPT_BODY",BODY,{"disambiguationData":[OSD([sQuery(id+"F0.wireOp",EDGE,"E1")])]}),"instanceName":"1"}),"instanceName":"1"}),"instanceName":"1"}),"instanceName":"1"}),"instanceName":"1"});
            var Q502;
            Q502=makeQuery(id+"F11.opPattern","COPY",BODY,{"derivedFrom":makeQuery(id+"F9.opPattern","COPY",BODY,{"derivedFrom":makeQuery(id+"F6.opPattern","COPY",BODY,{"derivedFrom":makeQuery(id+"F5.opPattern","COPY",BODY,{"derivedFrom":makeQuery(id+"F4.opPattern","COPY",BODY,{"derivedFrom":makeQuery(id+"F2.opPattern","COPY",BODY,{"derivedFrom":makeQuery(id+"F1.opRevolve","SWEPT_BODY",BODY,{"disambiguationData":[OSD([sQuery(id+"F0.wireOp",EDGE,"E1")])]}),"instanceName":"1"}),"instanceName":"1"}),"instanceName":"1"}),"instanceName":"1"}),"instanceName":"1"}),"instanceName":"1"});
            var Q503;
            Q503=makeQuery(id+"F11.opPattern","COPY",BODY,{"derivedFrom":makeQuery(id+"F9.opPattern","COPY",BODY,{"derivedFrom":makeQuery(id+"F6.opPattern","COPY",BODY,{"derivedFrom":makeQuery(id+"F5.opPattern","COPY",BODY,{"derivedFrom":makeQuery(id+"F4.opPattern","COPY",BODY,{"derivedFrom":makeQuery(id+"F3.opPattern","COPY",BODY,{"derivedFrom":makeQuery(id+"F2.opPattern","COPY",BODY,{"derivedFrom":makeQuery(id+"F1.opRevolve","SWEPT_BODY",BODY,{"disambiguationData":[OSD([sQuery(id+"F0.wireOp",EDGE,"E1")])]}),"instanceName":"1"}),"instanceName":"1"}),"instanceName":"1"}),"instanceName":"1"}),"instanceName":"1"}),"instanceName":"1"}),"instanceName":"1"});
            var Q504;
            Q504=makeQuery(id+"F11.opPattern","COPY",BODY,{"derivedFrom":makeQuery(id+"F9.opPattern","COPY",BODY,{"derivedFrom":makeQuery(id+"F7.opPattern","COPY",BODY,{"derivedFrom":makeQuery(id+"F1.opRevolve","SWEPT_BODY",BODY,{"disambiguationData":[OSD([sQuery(id+"F0.wireOp",EDGE,"E1")])]}),"instanceName":"1"}),"instanceName":"1"}),"instanceName":"1"});
            var Q505;
            Q505=makeQuery(id+"F11.opPattern","COPY",BODY,{"derivedFrom":makeQuery(id+"F9.opPattern","COPY",BODY,{"derivedFrom":makeQuery(id+"F7.opPattern","COPY",BODY,{"derivedFrom":makeQuery(id+"F2.opPattern","COPY",BODY,{"derivedFrom":makeQuery(id+"F1.opRevolve","SWEPT_BODY",BODY,{"disambiguationData":[OSD([sQuery(id+"F0.wireOp",EDGE,"E1")])]}),"instanceName":"1"}),"instanceName":"1"}),"instanceName":"1"}),"instanceName":"1"});
            var Q506;
            Q506=makeQuery(id+"F11.opPattern","COPY",BODY,{"derivedFrom":makeQuery(id+"F9.opPattern","COPY",BODY,{"derivedFrom":makeQuery(id+"F7.opPattern","COPY",BODY,{"derivedFrom":makeQuery(id+"F3.opPattern","COPY",BODY,{"derivedFrom":makeQuery(id+"F2.opPattern","COPY",BODY,{"derivedFrom":makeQuery(id+"F1.opRevolve","SWEPT_BODY",BODY,{"disambiguationData":[OSD([sQuery(id+"F0.wireOp",EDGE,"E1")])]}),"instanceName":"1"}),"instanceName":"1"}),"instanceName":"1"}),"instanceName":"1"}),"instanceName":"1"});
            var Q507;
            Q507=makeQuery(id+"F11.opPattern","COPY",BODY,{"derivedFrom":makeQuery(id+"F9.opPattern","COPY",BODY,{"derivedFrom":makeQuery(id+"F7.opPattern","COPY",BODY,{"derivedFrom":makeQuery(id+"F4.opPattern","COPY",BODY,{"derivedFrom":makeQuery(id+"F1.opRevolve","SWEPT_BODY",BODY,{"disambiguationData":[OSD([sQuery(id+"F0.wireOp",EDGE,"E1")])]}),"instanceName":"1"}),"instanceName":"1"}),"instanceName":"1"}),"instanceName":"1"});
            var Q508;
            Q508=makeQuery(id+"F11.opPattern","COPY",BODY,{"derivedFrom":makeQuery(id+"F9.opPattern","COPY",BODY,{"derivedFrom":makeQuery(id+"F7.opPattern","COPY",BODY,{"derivedFrom":makeQuery(id+"F4.opPattern","COPY",BODY,{"derivedFrom":makeQuery(id+"F2.opPattern","COPY",BODY,{"derivedFrom":makeQuery(id+"F1.opRevolve","SWEPT_BODY",BODY,{"disambiguationData":[OSD([sQuery(id+"F0.wireOp",EDGE,"E1")])]}),"instanceName":"1"}),"instanceName":"1"}),"instanceName":"1"}),"instanceName":"1"}),"instanceName":"1"});
            var Q509;
            Q509=makeQuery(id+"F11.opPattern","COPY",BODY,{"derivedFrom":makeQuery(id+"F9.opPattern","COPY",BODY,{"derivedFrom":makeQuery(id+"F7.opPattern","COPY",BODY,{"derivedFrom":makeQuery(id+"F4.opPattern","COPY",BODY,{"derivedFrom":makeQuery(id+"F3.opPattern","COPY",BODY,{"derivedFrom":makeQuery(id+"F2.opPattern","COPY",BODY,{"derivedFrom":makeQuery(id+"F1.opRevolve","SWEPT_BODY",BODY,{"disambiguationData":[OSD([sQuery(id+"F0.wireOp",EDGE,"E1")])]}),"instanceName":"1"}),"instanceName":"1"}),"instanceName":"1"}),"instanceName":"1"}),"instanceName":"1"}),"instanceName":"1"});
            var Q510;
            Q510=makeQuery(id+"F11.opPattern","COPY",BODY,{"derivedFrom":makeQuery(id+"F9.opPattern","COPY",BODY,{"derivedFrom":makeQuery(id+"F7.opPattern","COPY",BODY,{"derivedFrom":makeQuery(id+"F5.opPattern","COPY",BODY,{"derivedFrom":makeQuery(id+"F1.opRevolve","SWEPT_BODY",BODY,{"disambiguationData":[OSD([sQuery(id+"F0.wireOp",EDGE,"E1")])]}),"instanceName":"1"}),"instanceName":"1"}),"instanceName":"1"}),"instanceName":"1"});
            var Q511;
            Q511=makeQuery(id+"F11.opPattern","COPY",BODY,{"derivedFrom":makeQuery(id+"F9.opPattern","COPY",BODY,{"derivedFrom":makeQuery(id+"F7.opPattern","COPY",BODY,{"derivedFrom":makeQuery(id+"F5.opPattern","COPY",BODY,{"derivedFrom":makeQuery(id+"F2.opPattern","COPY",BODY,{"derivedFrom":makeQuery(id+"F1.opRevolve","SWEPT_BODY",BODY,{"disambiguationData":[OSD([sQuery(id+"F0.wireOp",EDGE,"E1")])]}),"instanceName":"1"}),"instanceName":"1"}),"instanceName":"1"}),"instanceName":"1"}),"instanceName":"1"});
            var Q512;
            Q512=makeQuery(id+"F11.opPattern","COPY",BODY,{"derivedFrom":makeQuery(id+"F9.opPattern","COPY",BODY,{"derivedFrom":makeQuery(id+"F7.opPattern","COPY",BODY,{"derivedFrom":makeQuery(id+"F5.opPattern","COPY",BODY,{"derivedFrom":makeQuery(id+"F3.opPattern","COPY",BODY,{"derivedFrom":makeQuery(id+"F2.opPattern","COPY",BODY,{"derivedFrom":makeQuery(id+"F1.opRevolve","SWEPT_BODY",BODY,{"disambiguationData":[OSD([sQuery(id+"F0.wireOp",EDGE,"E1")])]}),"instanceName":"1"}),"instanceName":"1"}),"instanceName":"1"}),"instanceName":"1"}),"instanceName":"1"}),"instanceName":"1"});
            var Q513;
            Q513=makeQuery(id+"F11.opPattern","COPY",BODY,{"derivedFrom":makeQuery(id+"F9.opPattern","COPY",BODY,{"derivedFrom":makeQuery(id+"F7.opPattern","COPY",BODY,{"derivedFrom":makeQuery(id+"F5.opPattern","COPY",BODY,{"derivedFrom":makeQuery(id+"F4.opPattern","COPY",BODY,{"derivedFrom":makeQuery(id+"F1.opRevolve","SWEPT_BODY",BODY,{"disambiguationData":[OSD([sQuery(id+"F0.wireOp",EDGE,"E1")])]}),"instanceName":"1"}),"instanceName":"1"}),"instanceName":"1"}),"instanceName":"1"}),"instanceName":"1"});
            var Q514;
            Q514=makeQuery(id+"F11.opPattern","COPY",BODY,{"derivedFrom":makeQuery(id+"F9.opPattern","COPY",BODY,{"derivedFrom":makeQuery(id+"F7.opPattern","COPY",BODY,{"derivedFrom":makeQuery(id+"F5.opPattern","COPY",BODY,{"derivedFrom":makeQuery(id+"F4.opPattern","COPY",BODY,{"derivedFrom":makeQuery(id+"F2.opPattern","COPY",BODY,{"derivedFrom":makeQuery(id+"F1.opRevolve","SWEPT_BODY",BODY,{"disambiguationData":[OSD([sQuery(id+"F0.wireOp",EDGE,"E1")])]}),"instanceName":"1"}),"instanceName":"1"}),"instanceName":"1"}),"instanceName":"1"}),"instanceName":"1"}),"instanceName":"1"});
            var Q515;
            Q515=makeQuery(id+"F11.opPattern","COPY",BODY,{"derivedFrom":makeQuery(id+"F9.opPattern","COPY",BODY,{"derivedFrom":makeQuery(id+"F7.opPattern","COPY",BODY,{"derivedFrom":makeQuery(id+"F5.opPattern","COPY",BODY,{"derivedFrom":makeQuery(id+"F4.opPattern","COPY",BODY,{"derivedFrom":makeQuery(id+"F3.opPattern","COPY",BODY,{"derivedFrom":makeQuery(id+"F2.opPattern","COPY",BODY,{"derivedFrom":makeQuery(id+"F1.opRevolve","SWEPT_BODY",BODY,{"disambiguationData":[OSD([sQuery(id+"F0.wireOp",EDGE,"E1")])]}),"instanceName":"1"}),"instanceName":"1"}),"instanceName":"1"}),"instanceName":"1"}),"instanceName":"1"}),"instanceName":"1"}),"instanceName":"1"});
            var Q516;
            Q516=makeQuery(id+"F11.opPattern","COPY",BODY,{"derivedFrom":makeQuery(id+"F9.opPattern","COPY",BODY,{"derivedFrom":makeQuery(id+"F7.opPattern","COPY",BODY,{"derivedFrom":makeQuery(id+"F6.opPattern","COPY",BODY,{"derivedFrom":makeQuery(id+"F1.opRevolve","SWEPT_BODY",BODY,{"disambiguationData":[OSD([sQuery(id+"F0.wireOp",EDGE,"E1")])]}),"instanceName":"1"}),"instanceName":"1"}),"instanceName":"1"}),"instanceName":"1"});
            var Q517;
            Q517=makeQuery(id+"F11.opPattern","COPY",BODY,{"derivedFrom":makeQuery(id+"F9.opPattern","COPY",BODY,{"derivedFrom":makeQuery(id+"F7.opPattern","COPY",BODY,{"derivedFrom":makeQuery(id+"F6.opPattern","COPY",BODY,{"derivedFrom":makeQuery(id+"F2.opPattern","COPY",BODY,{"derivedFrom":makeQuery(id+"F1.opRevolve","SWEPT_BODY",BODY,{"disambiguationData":[OSD([sQuery(id+"F0.wireOp",EDGE,"E1")])]}),"instanceName":"1"}),"instanceName":"1"}),"instanceName":"1"}),"instanceName":"1"}),"instanceName":"1"});
            var Q518;
            Q518=makeQuery(id+"F11.opPattern","COPY",BODY,{"derivedFrom":makeQuery(id+"F9.opPattern","COPY",BODY,{"derivedFrom":makeQuery(id+"F7.opPattern","COPY",BODY,{"derivedFrom":makeQuery(id+"F6.opPattern","COPY",BODY,{"derivedFrom":makeQuery(id+"F3.opPattern","COPY",BODY,{"derivedFrom":makeQuery(id+"F2.opPattern","COPY",BODY,{"derivedFrom":makeQuery(id+"F1.opRevolve","SWEPT_BODY",BODY,{"disambiguationData":[OSD([sQuery(id+"F0.wireOp",EDGE,"E1")])]}),"instanceName":"1"}),"instanceName":"1"}),"instanceName":"1"}),"instanceName":"1"}),"instanceName":"1"}),"instanceName":"1"});
            var Q519;
            Q519=makeQuery(id+"F11.opPattern","COPY",BODY,{"derivedFrom":makeQuery(id+"F9.opPattern","COPY",BODY,{"derivedFrom":makeQuery(id+"F7.opPattern","COPY",BODY,{"derivedFrom":makeQuery(id+"F6.opPattern","COPY",BODY,{"derivedFrom":makeQuery(id+"F4.opPattern","COPY",BODY,{"derivedFrom":makeQuery(id+"F1.opRevolve","SWEPT_BODY",BODY,{"disambiguationData":[OSD([sQuery(id+"F0.wireOp",EDGE,"E1")])]}),"instanceName":"1"}),"instanceName":"1"}),"instanceName":"1"}),"instanceName":"1"}),"instanceName":"1"});
            var Q520;
            Q520=makeQuery(id+"F11.opPattern","COPY",BODY,{"derivedFrom":makeQuery(id+"F9.opPattern","COPY",BODY,{"derivedFrom":makeQuery(id+"F7.opPattern","COPY",BODY,{"derivedFrom":makeQuery(id+"F6.opPattern","COPY",BODY,{"derivedFrom":makeQuery(id+"F4.opPattern","COPY",BODY,{"derivedFrom":makeQuery(id+"F2.opPattern","COPY",BODY,{"derivedFrom":makeQuery(id+"F1.opRevolve","SWEPT_BODY",BODY,{"disambiguationData":[OSD([sQuery(id+"F0.wireOp",EDGE,"E1")])]}),"instanceName":"1"}),"instanceName":"1"}),"instanceName":"1"}),"instanceName":"1"}),"instanceName":"1"}),"instanceName":"1"});
            var Q521;
            Q521=makeQuery(id+"F11.opPattern","COPY",BODY,{"derivedFrom":makeQuery(id+"F9.opPattern","COPY",BODY,{"derivedFrom":makeQuery(id+"F7.opPattern","COPY",BODY,{"derivedFrom":makeQuery(id+"F6.opPattern","COPY",BODY,{"derivedFrom":makeQuery(id+"F4.opPattern","COPY",BODY,{"derivedFrom":makeQuery(id+"F3.opPattern","COPY",BODY,{"derivedFrom":makeQuery(id+"F2.opPattern","COPY",BODY,{"derivedFrom":makeQuery(id+"F1.opRevolve","SWEPT_BODY",BODY,{"disambiguationData":[OSD([sQuery(id+"F0.wireOp",EDGE,"E1")])]}),"instanceName":"1"}),"instanceName":"1"}),"instanceName":"1"}),"instanceName":"1"}),"instanceName":"1"}),"instanceName":"1"}),"instanceName":"1"});
            var Q522;
            Q522=makeQuery(id+"F11.opPattern","COPY",BODY,{"derivedFrom":makeQuery(id+"F9.opPattern","COPY",BODY,{"derivedFrom":makeQuery(id+"F7.opPattern","COPY",BODY,{"derivedFrom":makeQuery(id+"F6.opPattern","COPY",BODY,{"derivedFrom":makeQuery(id+"F5.opPattern","COPY",BODY,{"derivedFrom":makeQuery(id+"F1.opRevolve","SWEPT_BODY",BODY,{"disambiguationData":[OSD([sQuery(id+"F0.wireOp",EDGE,"E1")])]}),"instanceName":"1"}),"instanceName":"1"}),"instanceName":"1"}),"instanceName":"1"}),"instanceName":"1"});
            var Q523;
            Q523=makeQuery(id+"F11.opPattern","COPY",BODY,{"derivedFrom":makeQuery(id+"F9.opPattern","COPY",BODY,{"derivedFrom":makeQuery(id+"F7.opPattern","COPY",BODY,{"derivedFrom":makeQuery(id+"F6.opPattern","COPY",BODY,{"derivedFrom":makeQuery(id+"F5.opPattern","COPY",BODY,{"derivedFrom":makeQuery(id+"F2.opPattern","COPY",BODY,{"derivedFrom":makeQuery(id+"F1.opRevolve","SWEPT_BODY",BODY,{"disambiguationData":[OSD([sQuery(id+"F0.wireOp",EDGE,"E1")])]}),"instanceName":"1"}),"instanceName":"1"}),"instanceName":"1"}),"instanceName":"1"}),"instanceName":"1"}),"instanceName":"1"});
            var Q524;
            Q524=makeQuery(id+"F11.opPattern","COPY",BODY,{"derivedFrom":makeQuery(id+"F9.opPattern","COPY",BODY,{"derivedFrom":makeQuery(id+"F7.opPattern","COPY",BODY,{"derivedFrom":makeQuery(id+"F6.opPattern","COPY",BODY,{"derivedFrom":makeQuery(id+"F5.opPattern","COPY",BODY,{"derivedFrom":makeQuery(id+"F3.opPattern","COPY",BODY,{"derivedFrom":makeQuery(id+"F2.opPattern","COPY",BODY,{"derivedFrom":makeQuery(id+"F1.opRevolve","SWEPT_BODY",BODY,{"disambiguationData":[OSD([sQuery(id+"F0.wireOp",EDGE,"E1")])]}),"instanceName":"1"}),"instanceName":"1"}),"instanceName":"1"}),"instanceName":"1"}),"instanceName":"1"}),"instanceName":"1"}),"instanceName":"1"});
            var Q525;
            Q525=makeQuery(id+"F11.opPattern","COPY",BODY,{"derivedFrom":makeQuery(id+"F9.opPattern","COPY",BODY,{"derivedFrom":makeQuery(id+"F7.opPattern","COPY",BODY,{"derivedFrom":makeQuery(id+"F6.opPattern","COPY",BODY,{"derivedFrom":makeQuery(id+"F5.opPattern","COPY",BODY,{"derivedFrom":makeQuery(id+"F4.opPattern","COPY",BODY,{"derivedFrom":makeQuery(id+"F1.opRevolve","SWEPT_BODY",BODY,{"disambiguationData":[OSD([sQuery(id+"F0.wireOp",EDGE,"E1")])]}),"instanceName":"1"}),"instanceName":"1"}),"instanceName":"1"}),"instanceName":"1"}),"instanceName":"1"}),"instanceName":"1"});
            var Q526;
            Q526=makeQuery(id+"F11.opPattern","COPY",BODY,{"derivedFrom":makeQuery(id+"F9.opPattern","COPY",BODY,{"derivedFrom":makeQuery(id+"F7.opPattern","COPY",BODY,{"derivedFrom":makeQuery(id+"F6.opPattern","COPY",BODY,{"derivedFrom":makeQuery(id+"F5.opPattern","COPY",BODY,{"derivedFrom":makeQuery(id+"F4.opPattern","COPY",BODY,{"derivedFrom":makeQuery(id+"F2.opPattern","COPY",BODY,{"derivedFrom":makeQuery(id+"F1.opRevolve","SWEPT_BODY",BODY,{"disambiguationData":[OSD([sQuery(id+"F0.wireOp",EDGE,"E1")])]}),"instanceName":"1"}),"instanceName":"1"}),"instanceName":"1"}),"instanceName":"1"}),"instanceName":"1"}),"instanceName":"1"}),"instanceName":"1"});
            var Q527;
            Q527=makeQuery(id+"F11.opPattern","COPY",BODY,{"derivedFrom":makeQuery(id+"F9.opPattern","COPY",BODY,{"derivedFrom":makeQuery(id+"F7.opPattern","COPY",BODY,{"derivedFrom":makeQuery(id+"F6.opPattern","COPY",BODY,{"derivedFrom":makeQuery(id+"F5.opPattern","COPY",BODY,{"derivedFrom":makeQuery(id+"F4.opPattern","COPY",BODY,{"derivedFrom":makeQuery(id+"F3.opPattern","COPY",BODY,{"derivedFrom":makeQuery(id+"F2.opPattern","COPY",BODY,{"derivedFrom":makeQuery(id+"F1.opRevolve","SWEPT_BODY",BODY,{"disambiguationData":[OSD([sQuery(id+"F0.wireOp",EDGE,"E1")])]}),"instanceName":"1"}),"instanceName":"1"}),"instanceName":"1"}),"instanceName":"1"}),"instanceName":"1"}),"instanceName":"1"}),"instanceName":"1"}),"instanceName":"1"});
            var Q528;
            Q528=makeQuery(id+"F11.opPattern","COPY",BODY,{"derivedFrom":makeQuery(id+"F9.opPattern","COPY",BODY,{"derivedFrom":makeQuery(id+"F8.opPattern","COPY",BODY,{"derivedFrom":makeQuery(id+"F1.opRevolve","SWEPT_BODY",BODY,{"disambiguationData":[OSD([sQuery(id+"F0.wireOp",EDGE,"E1")])]}),"instanceName":"1"}),"instanceName":"1"}),"instanceName":"1"});
            var Q529;
            Q529=makeQuery(id+"F11.opPattern","COPY",BODY,{"derivedFrom":makeQuery(id+"F9.opPattern","COPY",BODY,{"derivedFrom":makeQuery(id+"F8.opPattern","COPY",BODY,{"derivedFrom":makeQuery(id+"F2.opPattern","COPY",BODY,{"derivedFrom":makeQuery(id+"F1.opRevolve","SWEPT_BODY",BODY,{"disambiguationData":[OSD([sQuery(id+"F0.wireOp",EDGE,"E1")])]}),"instanceName":"1"}),"instanceName":"1"}),"instanceName":"1"}),"instanceName":"1"});
            var Q530;
            Q530=makeQuery(id+"F11.opPattern","COPY",BODY,{"derivedFrom":makeQuery(id+"F9.opPattern","COPY",BODY,{"derivedFrom":makeQuery(id+"F8.opPattern","COPY",BODY,{"derivedFrom":makeQuery(id+"F3.opPattern","COPY",BODY,{"derivedFrom":makeQuery(id+"F2.opPattern","COPY",BODY,{"derivedFrom":makeQuery(id+"F1.opRevolve","SWEPT_BODY",BODY,{"disambiguationData":[OSD([sQuery(id+"F0.wireOp",EDGE,"E1")])]}),"instanceName":"1"}),"instanceName":"1"}),"instanceName":"1"}),"instanceName":"1"}),"instanceName":"1"});
            var Q531;
            Q531=makeQuery(id+"F11.opPattern","COPY",BODY,{"derivedFrom":makeQuery(id+"F9.opPattern","COPY",BODY,{"derivedFrom":makeQuery(id+"F8.opPattern","COPY",BODY,{"derivedFrom":makeQuery(id+"F4.opPattern","COPY",BODY,{"derivedFrom":makeQuery(id+"F1.opRevolve","SWEPT_BODY",BODY,{"disambiguationData":[OSD([sQuery(id+"F0.wireOp",EDGE,"E1")])]}),"instanceName":"1"}),"instanceName":"1"}),"instanceName":"1"}),"instanceName":"1"});
            var Q532;
            Q532=makeQuery(id+"F11.opPattern","COPY",BODY,{"derivedFrom":makeQuery(id+"F9.opPattern","COPY",BODY,{"derivedFrom":makeQuery(id+"F8.opPattern","COPY",BODY,{"derivedFrom":makeQuery(id+"F4.opPattern","COPY",BODY,{"derivedFrom":makeQuery(id+"F2.opPattern","COPY",BODY,{"derivedFrom":makeQuery(id+"F1.opRevolve","SWEPT_BODY",BODY,{"disambiguationData":[OSD([sQuery(id+"F0.wireOp",EDGE,"E1")])]}),"instanceName":"1"}),"instanceName":"1"}),"instanceName":"1"}),"instanceName":"1"}),"instanceName":"1"});
            var Q533;
            Q533=makeQuery(id+"F11.opPattern","COPY",BODY,{"derivedFrom":makeQuery(id+"F9.opPattern","COPY",BODY,{"derivedFrom":makeQuery(id+"F8.opPattern","COPY",BODY,{"derivedFrom":makeQuery(id+"F4.opPattern","COPY",BODY,{"derivedFrom":makeQuery(id+"F3.opPattern","COPY",BODY,{"derivedFrom":makeQuery(id+"F2.opPattern","COPY",BODY,{"derivedFrom":makeQuery(id+"F1.opRevolve","SWEPT_BODY",BODY,{"disambiguationData":[OSD([sQuery(id+"F0.wireOp",EDGE,"E1")])]}),"instanceName":"1"}),"instanceName":"1"}),"instanceName":"1"}),"instanceName":"1"}),"instanceName":"1"}),"instanceName":"1"});
            var Q534;
            Q534=makeQuery(id+"F11.opPattern","COPY",BODY,{"derivedFrom":makeQuery(id+"F9.opPattern","COPY",BODY,{"derivedFrom":makeQuery(id+"F8.opPattern","COPY",BODY,{"derivedFrom":makeQuery(id+"F5.opPattern","COPY",BODY,{"derivedFrom":makeQuery(id+"F1.opRevolve","SWEPT_BODY",BODY,{"disambiguationData":[OSD([sQuery(id+"F0.wireOp",EDGE,"E1")])]}),"instanceName":"1"}),"instanceName":"1"}),"instanceName":"1"}),"instanceName":"1"});
            var Q535;
            Q535=makeQuery(id+"F11.opPattern","COPY",BODY,{"derivedFrom":makeQuery(id+"F9.opPattern","COPY",BODY,{"derivedFrom":makeQuery(id+"F8.opPattern","COPY",BODY,{"derivedFrom":makeQuery(id+"F5.opPattern","COPY",BODY,{"derivedFrom":makeQuery(id+"F2.opPattern","COPY",BODY,{"derivedFrom":makeQuery(id+"F1.opRevolve","SWEPT_BODY",BODY,{"disambiguationData":[OSD([sQuery(id+"F0.wireOp",EDGE,"E1")])]}),"instanceName":"1"}),"instanceName":"1"}),"instanceName":"1"}),"instanceName":"1"}),"instanceName":"1"});
            var Q536;
            Q536=makeQuery(id+"F11.opPattern","COPY",BODY,{"derivedFrom":makeQuery(id+"F9.opPattern","COPY",BODY,{"derivedFrom":makeQuery(id+"F8.opPattern","COPY",BODY,{"derivedFrom":makeQuery(id+"F5.opPattern","COPY",BODY,{"derivedFrom":makeQuery(id+"F3.opPattern","COPY",BODY,{"derivedFrom":makeQuery(id+"F2.opPattern","COPY",BODY,{"derivedFrom":makeQuery(id+"F1.opRevolve","SWEPT_BODY",BODY,{"disambiguationData":[OSD([sQuery(id+"F0.wireOp",EDGE,"E1")])]}),"instanceName":"1"}),"instanceName":"1"}),"instanceName":"1"}),"instanceName":"1"}),"instanceName":"1"}),"instanceName":"1"});
            var Q537;
            Q537=makeQuery(id+"F11.opPattern","COPY",BODY,{"derivedFrom":makeQuery(id+"F9.opPattern","COPY",BODY,{"derivedFrom":makeQuery(id+"F8.opPattern","COPY",BODY,{"derivedFrom":makeQuery(id+"F5.opPattern","COPY",BODY,{"derivedFrom":makeQuery(id+"F4.opPattern","COPY",BODY,{"derivedFrom":makeQuery(id+"F1.opRevolve","SWEPT_BODY",BODY,{"disambiguationData":[OSD([sQuery(id+"F0.wireOp",EDGE,"E1")])]}),"instanceName":"1"}),"instanceName":"1"}),"instanceName":"1"}),"instanceName":"1"}),"instanceName":"1"});
            var Q538;
            Q538=makeQuery(id+"F11.opPattern","COPY",BODY,{"derivedFrom":makeQuery(id+"F9.opPattern","COPY",BODY,{"derivedFrom":makeQuery(id+"F8.opPattern","COPY",BODY,{"derivedFrom":makeQuery(id+"F5.opPattern","COPY",BODY,{"derivedFrom":makeQuery(id+"F4.opPattern","COPY",BODY,{"derivedFrom":makeQuery(id+"F2.opPattern","COPY",BODY,{"derivedFrom":makeQuery(id+"F1.opRevolve","SWEPT_BODY",BODY,{"disambiguationData":[OSD([sQuery(id+"F0.wireOp",EDGE,"E1")])]}),"instanceName":"1"}),"instanceName":"1"}),"instanceName":"1"}),"instanceName":"1"}),"instanceName":"1"}),"instanceName":"1"});
            var Q539;
            Q539=makeQuery(id+"F11.opPattern","COPY",BODY,{"derivedFrom":makeQuery(id+"F9.opPattern","COPY",BODY,{"derivedFrom":makeQuery(id+"F8.opPattern","COPY",BODY,{"derivedFrom":makeQuery(id+"F5.opPattern","COPY",BODY,{"derivedFrom":makeQuery(id+"F4.opPattern","COPY",BODY,{"derivedFrom":makeQuery(id+"F3.opPattern","COPY",BODY,{"derivedFrom":makeQuery(id+"F2.opPattern","COPY",BODY,{"derivedFrom":makeQuery(id+"F1.opRevolve","SWEPT_BODY",BODY,{"disambiguationData":[OSD([sQuery(id+"F0.wireOp",EDGE,"E1")])]}),"instanceName":"1"}),"instanceName":"1"}),"instanceName":"1"}),"instanceName":"1"}),"instanceName":"1"}),"instanceName":"1"}),"instanceName":"1"});
            var Q540;
            Q540=makeQuery(id+"F11.opPattern","COPY",BODY,{"derivedFrom":makeQuery(id+"F9.opPattern","COPY",BODY,{"derivedFrom":makeQuery(id+"F8.opPattern","COPY",BODY,{"derivedFrom":makeQuery(id+"F6.opPattern","COPY",BODY,{"derivedFrom":makeQuery(id+"F1.opRevolve","SWEPT_BODY",BODY,{"disambiguationData":[OSD([sQuery(id+"F0.wireOp",EDGE,"E1")])]}),"instanceName":"1"}),"instanceName":"1"}),"instanceName":"1"}),"instanceName":"1"});
            var Q541;
            Q541=makeQuery(id+"F11.opPattern","COPY",BODY,{"derivedFrom":makeQuery(id+"F9.opPattern","COPY",BODY,{"derivedFrom":makeQuery(id+"F8.opPattern","COPY",BODY,{"derivedFrom":makeQuery(id+"F6.opPattern","COPY",BODY,{"derivedFrom":makeQuery(id+"F2.opPattern","COPY",BODY,{"derivedFrom":makeQuery(id+"F1.opRevolve","SWEPT_BODY",BODY,{"disambiguationData":[OSD([sQuery(id+"F0.wireOp",EDGE,"E1")])]}),"instanceName":"1"}),"instanceName":"1"}),"instanceName":"1"}),"instanceName":"1"}),"instanceName":"1"});
            var Q542;
            Q542=makeQuery(id+"F11.opPattern","COPY",BODY,{"derivedFrom":makeQuery(id+"F9.opPattern","COPY",BODY,{"derivedFrom":makeQuery(id+"F8.opPattern","COPY",BODY,{"derivedFrom":makeQuery(id+"F6.opPattern","COPY",BODY,{"derivedFrom":makeQuery(id+"F3.opPattern","COPY",BODY,{"derivedFrom":makeQuery(id+"F2.opPattern","COPY",BODY,{"derivedFrom":makeQuery(id+"F1.opRevolve","SWEPT_BODY",BODY,{"disambiguationData":[OSD([sQuery(id+"F0.wireOp",EDGE,"E1")])]}),"instanceName":"1"}),"instanceName":"1"}),"instanceName":"1"}),"instanceName":"1"}),"instanceName":"1"}),"instanceName":"1"});
            var Q543;
            Q543=makeQuery(id+"F11.opPattern","COPY",BODY,{"derivedFrom":makeQuery(id+"F9.opPattern","COPY",BODY,{"derivedFrom":makeQuery(id+"F8.opPattern","COPY",BODY,{"derivedFrom":makeQuery(id+"F6.opPattern","COPY",BODY,{"derivedFrom":makeQuery(id+"F4.opPattern","COPY",BODY,{"derivedFrom":makeQuery(id+"F1.opRevolve","SWEPT_BODY",BODY,{"disambiguationData":[OSD([sQuery(id+"F0.wireOp",EDGE,"E1")])]}),"instanceName":"1"}),"instanceName":"1"}),"instanceName":"1"}),"instanceName":"1"}),"instanceName":"1"});
            var Q544;
            Q544=makeQuery(id+"F11.opPattern","COPY",BODY,{"derivedFrom":makeQuery(id+"F9.opPattern","COPY",BODY,{"derivedFrom":makeQuery(id+"F8.opPattern","COPY",BODY,{"derivedFrom":makeQuery(id+"F6.opPattern","COPY",BODY,{"derivedFrom":makeQuery(id+"F4.opPattern","COPY",BODY,{"derivedFrom":makeQuery(id+"F2.opPattern","COPY",BODY,{"derivedFrom":makeQuery(id+"F1.opRevolve","SWEPT_BODY",BODY,{"disambiguationData":[OSD([sQuery(id+"F0.wireOp",EDGE,"E1")])]}),"instanceName":"1"}),"instanceName":"1"}),"instanceName":"1"}),"instanceName":"1"}),"instanceName":"1"}),"instanceName":"1"});
            var Q545;
            Q545=makeQuery(id+"F11.opPattern","COPY",BODY,{"derivedFrom":makeQuery(id+"F9.opPattern","COPY",BODY,{"derivedFrom":makeQuery(id+"F8.opPattern","COPY",BODY,{"derivedFrom":makeQuery(id+"F6.opPattern","COPY",BODY,{"derivedFrom":makeQuery(id+"F4.opPattern","COPY",BODY,{"derivedFrom":makeQuery(id+"F3.opPattern","COPY",BODY,{"derivedFrom":makeQuery(id+"F2.opPattern","COPY",BODY,{"derivedFrom":makeQuery(id+"F1.opRevolve","SWEPT_BODY",BODY,{"disambiguationData":[OSD([sQuery(id+"F0.wireOp",EDGE,"E1")])]}),"instanceName":"1"}),"instanceName":"1"}),"instanceName":"1"}),"instanceName":"1"}),"instanceName":"1"}),"instanceName":"1"}),"instanceName":"1"});
            var Q546;
            Q546=makeQuery(id+"F11.opPattern","COPY",BODY,{"derivedFrom":makeQuery(id+"F9.opPattern","COPY",BODY,{"derivedFrom":makeQuery(id+"F8.opPattern","COPY",BODY,{"derivedFrom":makeQuery(id+"F6.opPattern","COPY",BODY,{"derivedFrom":makeQuery(id+"F5.opPattern","COPY",BODY,{"derivedFrom":makeQuery(id+"F1.opRevolve","SWEPT_BODY",BODY,{"disambiguationData":[OSD([sQuery(id+"F0.wireOp",EDGE,"E1")])]}),"instanceName":"1"}),"instanceName":"1"}),"instanceName":"1"}),"instanceName":"1"}),"instanceName":"1"});
            var Q547;
            Q547=makeQuery(id+"F11.opPattern","COPY",BODY,{"derivedFrom":makeQuery(id+"F9.opPattern","COPY",BODY,{"derivedFrom":makeQuery(id+"F8.opPattern","COPY",BODY,{"derivedFrom":makeQuery(id+"F6.opPattern","COPY",BODY,{"derivedFrom":makeQuery(id+"F5.opPattern","COPY",BODY,{"derivedFrom":makeQuery(id+"F2.opPattern","COPY",BODY,{"derivedFrom":makeQuery(id+"F1.opRevolve","SWEPT_BODY",BODY,{"disambiguationData":[OSD([sQuery(id+"F0.wireOp",EDGE,"E1")])]}),"instanceName":"1"}),"instanceName":"1"}),"instanceName":"1"}),"instanceName":"1"}),"instanceName":"1"}),"instanceName":"1"});
            var Q548;
            Q548=makeQuery(id+"F11.opPattern","COPY",BODY,{"derivedFrom":makeQuery(id+"F9.opPattern","COPY",BODY,{"derivedFrom":makeQuery(id+"F8.opPattern","COPY",BODY,{"derivedFrom":makeQuery(id+"F6.opPattern","COPY",BODY,{"derivedFrom":makeQuery(id+"F5.opPattern","COPY",BODY,{"derivedFrom":makeQuery(id+"F3.opPattern","COPY",BODY,{"derivedFrom":makeQuery(id+"F2.opPattern","COPY",BODY,{"derivedFrom":makeQuery(id+"F1.opRevolve","SWEPT_BODY",BODY,{"disambiguationData":[OSD([sQuery(id+"F0.wireOp",EDGE,"E1")])]}),"instanceName":"1"}),"instanceName":"1"}),"instanceName":"1"}),"instanceName":"1"}),"instanceName":"1"}),"instanceName":"1"}),"instanceName":"1"});
            var Q549;
            Q549=makeQuery(id+"F11.opPattern","COPY",BODY,{"derivedFrom":makeQuery(id+"F9.opPattern","COPY",BODY,{"derivedFrom":makeQuery(id+"F8.opPattern","COPY",BODY,{"derivedFrom":makeQuery(id+"F6.opPattern","COPY",BODY,{"derivedFrom":makeQuery(id+"F5.opPattern","COPY",BODY,{"derivedFrom":makeQuery(id+"F4.opPattern","COPY",BODY,{"derivedFrom":makeQuery(id+"F1.opRevolve","SWEPT_BODY",BODY,{"disambiguationData":[OSD([sQuery(id+"F0.wireOp",EDGE,"E1")])]}),"instanceName":"1"}),"instanceName":"1"}),"instanceName":"1"}),"instanceName":"1"}),"instanceName":"1"}),"instanceName":"1"});
            var Q550;
            Q550=makeQuery(id+"F11.opPattern","COPY",BODY,{"derivedFrom":makeQuery(id+"F9.opPattern","COPY",BODY,{"derivedFrom":makeQuery(id+"F8.opPattern","COPY",BODY,{"derivedFrom":makeQuery(id+"F6.opPattern","COPY",BODY,{"derivedFrom":makeQuery(id+"F5.opPattern","COPY",BODY,{"derivedFrom":makeQuery(id+"F4.opPattern","COPY",BODY,{"derivedFrom":makeQuery(id+"F2.opPattern","COPY",BODY,{"derivedFrom":makeQuery(id+"F1.opRevolve","SWEPT_BODY",BODY,{"disambiguationData":[OSD([sQuery(id+"F0.wireOp",EDGE,"E1")])]}),"instanceName":"1"}),"instanceName":"1"}),"instanceName":"1"}),"instanceName":"1"}),"instanceName":"1"}),"instanceName":"1"}),"instanceName":"1"});
            var Q551;
            Q551=makeQuery(id+"F11.opPattern","COPY",BODY,{"derivedFrom":makeQuery(id+"F9.opPattern","COPY",BODY,{"derivedFrom":makeQuery(id+"F8.opPattern","COPY",BODY,{"derivedFrom":makeQuery(id+"F6.opPattern","COPY",BODY,{"derivedFrom":makeQuery(id+"F5.opPattern","COPY",BODY,{"derivedFrom":makeQuery(id+"F4.opPattern","COPY",BODY,{"derivedFrom":makeQuery(id+"F3.opPattern","COPY",BODY,{"derivedFrom":makeQuery(id+"F2.opPattern","COPY",BODY,{"derivedFrom":makeQuery(id+"F1.opRevolve","SWEPT_BODY",BODY,{"disambiguationData":[OSD([sQuery(id+"F0.wireOp",EDGE,"E1")])]}),"instanceName":"1"}),"instanceName":"1"}),"instanceName":"1"}),"instanceName":"1"}),"instanceName":"1"}),"instanceName":"1"}),"instanceName":"1"}),"instanceName":"1"});
            var Q552;
            Q552=makeQuery(id+"F11.opPattern","COPY",BODY,{"derivedFrom":makeQuery(id+"F9.opPattern","COPY",BODY,{"derivedFrom":makeQuery(id+"F8.opPattern","COPY",BODY,{"derivedFrom":makeQuery(id+"F7.opPattern","COPY",BODY,{"derivedFrom":makeQuery(id+"F1.opRevolve","SWEPT_BODY",BODY,{"disambiguationData":[OSD([sQuery(id+"F0.wireOp",EDGE,"E1")])]}),"instanceName":"1"}),"instanceName":"1"}),"instanceName":"1"}),"instanceName":"1"});
            var Q553;
            Q553=makeQuery(id+"F11.opPattern","COPY",BODY,{"derivedFrom":makeQuery(id+"F9.opPattern","COPY",BODY,{"derivedFrom":makeQuery(id+"F8.opPattern","COPY",BODY,{"derivedFrom":makeQuery(id+"F7.opPattern","COPY",BODY,{"derivedFrom":makeQuery(id+"F2.opPattern","COPY",BODY,{"derivedFrom":makeQuery(id+"F1.opRevolve","SWEPT_BODY",BODY,{"disambiguationData":[OSD([sQuery(id+"F0.wireOp",EDGE,"E1")])]}),"instanceName":"1"}),"instanceName":"1"}),"instanceName":"1"}),"instanceName":"1"}),"instanceName":"1"});
            var Q554;
            Q554=makeQuery(id+"F11.opPattern","COPY",BODY,{"derivedFrom":makeQuery(id+"F9.opPattern","COPY",BODY,{"derivedFrom":makeQuery(id+"F8.opPattern","COPY",BODY,{"derivedFrom":makeQuery(id+"F7.opPattern","COPY",BODY,{"derivedFrom":makeQuery(id+"F3.opPattern","COPY",BODY,{"derivedFrom":makeQuery(id+"F2.opPattern","COPY",BODY,{"derivedFrom":makeQuery(id+"F1.opRevolve","SWEPT_BODY",BODY,{"disambiguationData":[OSD([sQuery(id+"F0.wireOp",EDGE,"E1")])]}),"instanceName":"1"}),"instanceName":"1"}),"instanceName":"1"}),"instanceName":"1"}),"instanceName":"1"}),"instanceName":"1"});
            var Q555;
            Q555=makeQuery(id+"F11.opPattern","COPY",BODY,{"derivedFrom":makeQuery(id+"F9.opPattern","COPY",BODY,{"derivedFrom":makeQuery(id+"F8.opPattern","COPY",BODY,{"derivedFrom":makeQuery(id+"F7.opPattern","COPY",BODY,{"derivedFrom":makeQuery(id+"F4.opPattern","COPY",BODY,{"derivedFrom":makeQuery(id+"F1.opRevolve","SWEPT_BODY",BODY,{"disambiguationData":[OSD([sQuery(id+"F0.wireOp",EDGE,"E1")])]}),"instanceName":"1"}),"instanceName":"1"}),"instanceName":"1"}),"instanceName":"1"}),"instanceName":"1"});
            var Q556;
            Q556=makeQuery(id+"F11.opPattern","COPY",BODY,{"derivedFrom":makeQuery(id+"F9.opPattern","COPY",BODY,{"derivedFrom":makeQuery(id+"F8.opPattern","COPY",BODY,{"derivedFrom":makeQuery(id+"F7.opPattern","COPY",BODY,{"derivedFrom":makeQuery(id+"F4.opPattern","COPY",BODY,{"derivedFrom":makeQuery(id+"F2.opPattern","COPY",BODY,{"derivedFrom":makeQuery(id+"F1.opRevolve","SWEPT_BODY",BODY,{"disambiguationData":[OSD([sQuery(id+"F0.wireOp",EDGE,"E1")])]}),"instanceName":"1"}),"instanceName":"1"}),"instanceName":"1"}),"instanceName":"1"}),"instanceName":"1"}),"instanceName":"1"});
            var Q557;
            Q557=makeQuery(id+"F11.opPattern","COPY",BODY,{"derivedFrom":makeQuery(id+"F9.opPattern","COPY",BODY,{"derivedFrom":makeQuery(id+"F8.opPattern","COPY",BODY,{"derivedFrom":makeQuery(id+"F7.opPattern","COPY",BODY,{"derivedFrom":makeQuery(id+"F4.opPattern","COPY",BODY,{"derivedFrom":makeQuery(id+"F3.opPattern","COPY",BODY,{"derivedFrom":makeQuery(id+"F2.opPattern","COPY",BODY,{"derivedFrom":makeQuery(id+"F1.opRevolve","SWEPT_BODY",BODY,{"disambiguationData":[OSD([sQuery(id+"F0.wireOp",EDGE,"E1")])]}),"instanceName":"1"}),"instanceName":"1"}),"instanceName":"1"}),"instanceName":"1"}),"instanceName":"1"}),"instanceName":"1"}),"instanceName":"1"});
            var Q558;
            Q558=makeQuery(id+"F11.opPattern","COPY",BODY,{"derivedFrom":makeQuery(id+"F9.opPattern","COPY",BODY,{"derivedFrom":makeQuery(id+"F8.opPattern","COPY",BODY,{"derivedFrom":makeQuery(id+"F7.opPattern","COPY",BODY,{"derivedFrom":makeQuery(id+"F5.opPattern","COPY",BODY,{"derivedFrom":makeQuery(id+"F1.opRevolve","SWEPT_BODY",BODY,{"disambiguationData":[OSD([sQuery(id+"F0.wireOp",EDGE,"E1")])]}),"instanceName":"1"}),"instanceName":"1"}),"instanceName":"1"}),"instanceName":"1"}),"instanceName":"1"});
            var Q559;
            Q559=makeQuery(id+"F11.opPattern","COPY",BODY,{"derivedFrom":makeQuery(id+"F9.opPattern","COPY",BODY,{"derivedFrom":makeQuery(id+"F8.opPattern","COPY",BODY,{"derivedFrom":makeQuery(id+"F7.opPattern","COPY",BODY,{"derivedFrom":makeQuery(id+"F5.opPattern","COPY",BODY,{"derivedFrom":makeQuery(id+"F2.opPattern","COPY",BODY,{"derivedFrom":makeQuery(id+"F1.opRevolve","SWEPT_BODY",BODY,{"disambiguationData":[OSD([sQuery(id+"F0.wireOp",EDGE,"E1")])]}),"instanceName":"1"}),"instanceName":"1"}),"instanceName":"1"}),"instanceName":"1"}),"instanceName":"1"}),"instanceName":"1"});
            var Q560;
            Q560=makeQuery(id+"F11.opPattern","COPY",BODY,{"derivedFrom":makeQuery(id+"F9.opPattern","COPY",BODY,{"derivedFrom":makeQuery(id+"F8.opPattern","COPY",BODY,{"derivedFrom":makeQuery(id+"F7.opPattern","COPY",BODY,{"derivedFrom":makeQuery(id+"F5.opPattern","COPY",BODY,{"derivedFrom":makeQuery(id+"F3.opPattern","COPY",BODY,{"derivedFrom":makeQuery(id+"F2.opPattern","COPY",BODY,{"derivedFrom":makeQuery(id+"F1.opRevolve","SWEPT_BODY",BODY,{"disambiguationData":[OSD([sQuery(id+"F0.wireOp",EDGE,"E1")])]}),"instanceName":"1"}),"instanceName":"1"}),"instanceName":"1"}),"instanceName":"1"}),"instanceName":"1"}),"instanceName":"1"}),"instanceName":"1"});
            var Q561;
            Q561=makeQuery(id+"F11.opPattern","COPY",BODY,{"derivedFrom":makeQuery(id+"F9.opPattern","COPY",BODY,{"derivedFrom":makeQuery(id+"F8.opPattern","COPY",BODY,{"derivedFrom":makeQuery(id+"F7.opPattern","COPY",BODY,{"derivedFrom":makeQuery(id+"F5.opPattern","COPY",BODY,{"derivedFrom":makeQuery(id+"F4.opPattern","COPY",BODY,{"derivedFrom":makeQuery(id+"F1.opRevolve","SWEPT_BODY",BODY,{"disambiguationData":[OSD([sQuery(id+"F0.wireOp",EDGE,"E1")])]}),"instanceName":"1"}),"instanceName":"1"}),"instanceName":"1"}),"instanceName":"1"}),"instanceName":"1"}),"instanceName":"1"});
            var Q562;
            Q562=makeQuery(id+"F11.opPattern","COPY",BODY,{"derivedFrom":makeQuery(id+"F9.opPattern","COPY",BODY,{"derivedFrom":makeQuery(id+"F8.opPattern","COPY",BODY,{"derivedFrom":makeQuery(id+"F7.opPattern","COPY",BODY,{"derivedFrom":makeQuery(id+"F5.opPattern","COPY",BODY,{"derivedFrom":makeQuery(id+"F4.opPattern","COPY",BODY,{"derivedFrom":makeQuery(id+"F2.opPattern","COPY",BODY,{"derivedFrom":makeQuery(id+"F1.opRevolve","SWEPT_BODY",BODY,{"disambiguationData":[OSD([sQuery(id+"F0.wireOp",EDGE,"E1")])]}),"instanceName":"1"}),"instanceName":"1"}),"instanceName":"1"}),"instanceName":"1"}),"instanceName":"1"}),"instanceName":"1"}),"instanceName":"1"});
            var Q563;
            Q563=makeQuery(id+"F11.opPattern","COPY",BODY,{"derivedFrom":makeQuery(id+"F9.opPattern","COPY",BODY,{"derivedFrom":makeQuery(id+"F8.opPattern","COPY",BODY,{"derivedFrom":makeQuery(id+"F7.opPattern","COPY",BODY,{"derivedFrom":makeQuery(id+"F5.opPattern","COPY",BODY,{"derivedFrom":makeQuery(id+"F4.opPattern","COPY",BODY,{"derivedFrom":makeQuery(id+"F3.opPattern","COPY",BODY,{"derivedFrom":makeQuery(id+"F2.opPattern","COPY",BODY,{"derivedFrom":makeQuery(id+"F1.opRevolve","SWEPT_BODY",BODY,{"disambiguationData":[OSD([sQuery(id+"F0.wireOp",EDGE,"E1")])]}),"instanceName":"1"}),"instanceName":"1"}),"instanceName":"1"}),"instanceName":"1"}),"instanceName":"1"}),"instanceName":"1"}),"instanceName":"1"}),"instanceName":"1"});
            var Q564;
            Q564=makeQuery(id+"F11.opPattern","COPY",BODY,{"derivedFrom":makeQuery(id+"F9.opPattern","COPY",BODY,{"derivedFrom":makeQuery(id+"F8.opPattern","COPY",BODY,{"derivedFrom":makeQuery(id+"F7.opPattern","COPY",BODY,{"derivedFrom":makeQuery(id+"F6.opPattern","COPY",BODY,{"derivedFrom":makeQuery(id+"F1.opRevolve","SWEPT_BODY",BODY,{"disambiguationData":[OSD([sQuery(id+"F0.wireOp",EDGE,"E1")])]}),"instanceName":"1"}),"instanceName":"1"}),"instanceName":"1"}),"instanceName":"1"}),"instanceName":"1"});
            var Q565;
            Q565=makeQuery(id+"F11.opPattern","COPY",BODY,{"derivedFrom":makeQuery(id+"F9.opPattern","COPY",BODY,{"derivedFrom":makeQuery(id+"F8.opPattern","COPY",BODY,{"derivedFrom":makeQuery(id+"F7.opPattern","COPY",BODY,{"derivedFrom":makeQuery(id+"F6.opPattern","COPY",BODY,{"derivedFrom":makeQuery(id+"F2.opPattern","COPY",BODY,{"derivedFrom":makeQuery(id+"F1.opRevolve","SWEPT_BODY",BODY,{"disambiguationData":[OSD([sQuery(id+"F0.wireOp",EDGE,"E1")])]}),"instanceName":"1"}),"instanceName":"1"}),"instanceName":"1"}),"instanceName":"1"}),"instanceName":"1"}),"instanceName":"1"});
            var Q566;
            Q566=makeQuery(id+"F11.opPattern","COPY",BODY,{"derivedFrom":makeQuery(id+"F9.opPattern","COPY",BODY,{"derivedFrom":makeQuery(id+"F8.opPattern","COPY",BODY,{"derivedFrom":makeQuery(id+"F7.opPattern","COPY",BODY,{"derivedFrom":makeQuery(id+"F6.opPattern","COPY",BODY,{"derivedFrom":makeQuery(id+"F3.opPattern","COPY",BODY,{"derivedFrom":makeQuery(id+"F2.opPattern","COPY",BODY,{"derivedFrom":makeQuery(id+"F1.opRevolve","SWEPT_BODY",BODY,{"disambiguationData":[OSD([sQuery(id+"F0.wireOp",EDGE,"E1")])]}),"instanceName":"1"}),"instanceName":"1"}),"instanceName":"1"}),"instanceName":"1"}),"instanceName":"1"}),"instanceName":"1"}),"instanceName":"1"});
            var Q567;
            Q567=makeQuery(id+"F11.opPattern","COPY",BODY,{"derivedFrom":makeQuery(id+"F9.opPattern","COPY",BODY,{"derivedFrom":makeQuery(id+"F8.opPattern","COPY",BODY,{"derivedFrom":makeQuery(id+"F7.opPattern","COPY",BODY,{"derivedFrom":makeQuery(id+"F6.opPattern","COPY",BODY,{"derivedFrom":makeQuery(id+"F4.opPattern","COPY",BODY,{"derivedFrom":makeQuery(id+"F1.opRevolve","SWEPT_BODY",BODY,{"disambiguationData":[OSD([sQuery(id+"F0.wireOp",EDGE,"E1")])]}),"instanceName":"1"}),"instanceName":"1"}),"instanceName":"1"}),"instanceName":"1"}),"instanceName":"1"}),"instanceName":"1"});
            var Q568;
            Q568=makeQuery(id+"F11.opPattern","COPY",BODY,{"derivedFrom":makeQuery(id+"F9.opPattern","COPY",BODY,{"derivedFrom":makeQuery(id+"F8.opPattern","COPY",BODY,{"derivedFrom":makeQuery(id+"F7.opPattern","COPY",BODY,{"derivedFrom":makeQuery(id+"F6.opPattern","COPY",BODY,{"derivedFrom":makeQuery(id+"F4.opPattern","COPY",BODY,{"derivedFrom":makeQuery(id+"F2.opPattern","COPY",BODY,{"derivedFrom":makeQuery(id+"F1.opRevolve","SWEPT_BODY",BODY,{"disambiguationData":[OSD([sQuery(id+"F0.wireOp",EDGE,"E1")])]}),"instanceName":"1"}),"instanceName":"1"}),"instanceName":"1"}),"instanceName":"1"}),"instanceName":"1"}),"instanceName":"1"}),"instanceName":"1"});
            var Q569;
            Q569=makeQuery(id+"F11.opPattern","COPY",BODY,{"derivedFrom":makeQuery(id+"F9.opPattern","COPY",BODY,{"derivedFrom":makeQuery(id+"F8.opPattern","COPY",BODY,{"derivedFrom":makeQuery(id+"F7.opPattern","COPY",BODY,{"derivedFrom":makeQuery(id+"F6.opPattern","COPY",BODY,{"derivedFrom":makeQuery(id+"F4.opPattern","COPY",BODY,{"derivedFrom":makeQuery(id+"F3.opPattern","COPY",BODY,{"derivedFrom":makeQuery(id+"F2.opPattern","COPY",BODY,{"derivedFrom":makeQuery(id+"F1.opRevolve","SWEPT_BODY",BODY,{"disambiguationData":[OSD([sQuery(id+"F0.wireOp",EDGE,"E1")])]}),"instanceName":"1"}),"instanceName":"1"}),"instanceName":"1"}),"instanceName":"1"}),"instanceName":"1"}),"instanceName":"1"}),"instanceName":"1"}),"instanceName":"1"});
            var Q570;
            Q570=makeQuery(id+"F11.opPattern","COPY",BODY,{"derivedFrom":makeQuery(id+"F9.opPattern","COPY",BODY,{"derivedFrom":makeQuery(id+"F8.opPattern","COPY",BODY,{"derivedFrom":makeQuery(id+"F7.opPattern","COPY",BODY,{"derivedFrom":makeQuery(id+"F6.opPattern","COPY",BODY,{"derivedFrom":makeQuery(id+"F5.opPattern","COPY",BODY,{"derivedFrom":makeQuery(id+"F1.opRevolve","SWEPT_BODY",BODY,{"disambiguationData":[OSD([sQuery(id+"F0.wireOp",EDGE,"E1")])]}),"instanceName":"1"}),"instanceName":"1"}),"instanceName":"1"}),"instanceName":"1"}),"instanceName":"1"}),"instanceName":"1"});
            var Q571;
            Q571=makeQuery(id+"F11.opPattern","COPY",BODY,{"derivedFrom":makeQuery(id+"F9.opPattern","COPY",BODY,{"derivedFrom":makeQuery(id+"F8.opPattern","COPY",BODY,{"derivedFrom":makeQuery(id+"F7.opPattern","COPY",BODY,{"derivedFrom":makeQuery(id+"F6.opPattern","COPY",BODY,{"derivedFrom":makeQuery(id+"F5.opPattern","COPY",BODY,{"derivedFrom":makeQuery(id+"F2.opPattern","COPY",BODY,{"derivedFrom":makeQuery(id+"F1.opRevolve","SWEPT_BODY",BODY,{"disambiguationData":[OSD([sQuery(id+"F0.wireOp",EDGE,"E1")])]}),"instanceName":"1"}),"instanceName":"1"}),"instanceName":"1"}),"instanceName":"1"}),"instanceName":"1"}),"instanceName":"1"}),"instanceName":"1"});
            var Q572;
            Q572=makeQuery(id+"F11.opPattern","COPY",BODY,{"derivedFrom":makeQuery(id+"F9.opPattern","COPY",BODY,{"derivedFrom":makeQuery(id+"F8.opPattern","COPY",BODY,{"derivedFrom":makeQuery(id+"F7.opPattern","COPY",BODY,{"derivedFrom":makeQuery(id+"F6.opPattern","COPY",BODY,{"derivedFrom":makeQuery(id+"F5.opPattern","COPY",BODY,{"derivedFrom":makeQuery(id+"F3.opPattern","COPY",BODY,{"derivedFrom":makeQuery(id+"F2.opPattern","COPY",BODY,{"derivedFrom":makeQuery(id+"F1.opRevolve","SWEPT_BODY",BODY,{"disambiguationData":[OSD([sQuery(id+"F0.wireOp",EDGE,"E1")])]}),"instanceName":"1"}),"instanceName":"1"}),"instanceName":"1"}),"instanceName":"1"}),"instanceName":"1"}),"instanceName":"1"}),"instanceName":"1"}),"instanceName":"1"});
            var Q573;
            Q573=makeQuery(id+"F11.opPattern","COPY",BODY,{"derivedFrom":makeQuery(id+"F9.opPattern","COPY",BODY,{"derivedFrom":makeQuery(id+"F8.opPattern","COPY",BODY,{"derivedFrom":makeQuery(id+"F7.opPattern","COPY",BODY,{"derivedFrom":makeQuery(id+"F6.opPattern","COPY",BODY,{"derivedFrom":makeQuery(id+"F5.opPattern","COPY",BODY,{"derivedFrom":makeQuery(id+"F4.opPattern","COPY",BODY,{"derivedFrom":makeQuery(id+"F1.opRevolve","SWEPT_BODY",BODY,{"disambiguationData":[OSD([sQuery(id+"F0.wireOp",EDGE,"E1")])]}),"instanceName":"1"}),"instanceName":"1"}),"instanceName":"1"}),"instanceName":"1"}),"instanceName":"1"}),"instanceName":"1"}),"instanceName":"1"});
            var Q574;
            Q574=makeQuery(id+"F11.opPattern","COPY",BODY,{"derivedFrom":makeQuery(id+"F9.opPattern","COPY",BODY,{"derivedFrom":makeQuery(id+"F8.opPattern","COPY",BODY,{"derivedFrom":makeQuery(id+"F7.opPattern","COPY",BODY,{"derivedFrom":makeQuery(id+"F6.opPattern","COPY",BODY,{"derivedFrom":makeQuery(id+"F5.opPattern","COPY",BODY,{"derivedFrom":makeQuery(id+"F4.opPattern","COPY",BODY,{"derivedFrom":makeQuery(id+"F2.opPattern","COPY",BODY,{"derivedFrom":makeQuery(id+"F1.opRevolve","SWEPT_BODY",BODY,{"disambiguationData":[OSD([sQuery(id+"F0.wireOp",EDGE,"E1")])]}),"instanceName":"1"}),"instanceName":"1"}),"instanceName":"1"}),"instanceName":"1"}),"instanceName":"1"}),"instanceName":"1"}),"instanceName":"1"}),"instanceName":"1"});
            var Q575;
            Q575=makeQuery(id+"F11.opPattern","COPY",BODY,{"derivedFrom":makeQuery(id+"F9.opPattern","COPY",BODY,{"derivedFrom":makeQuery(id+"F8.opPattern","COPY",BODY,{"derivedFrom":makeQuery(id+"F7.opPattern","COPY",BODY,{"derivedFrom":makeQuery(id+"F6.opPattern","COPY",BODY,{"derivedFrom":makeQuery(id+"F5.opPattern","COPY",BODY,{"derivedFrom":makeQuery(id+"F4.opPattern","COPY",BODY,{"derivedFrom":makeQuery(id+"F3.opPattern","COPY",BODY,{"derivedFrom":makeQuery(id+"F2.opPattern","COPY",BODY,{"derivedFrom":makeQuery(id+"F1.opRevolve","SWEPT_BODY",BODY,{"disambiguationData":[OSD([sQuery(id+"F0.wireOp",EDGE,"E1")])]}),"instanceName":"1"}),"instanceName":"1"}),"instanceName":"1"}),"instanceName":"1"}),"instanceName":"1"}),"instanceName":"1"}),"instanceName":"1"}),"instanceName":"1"}),"instanceName":"1"});
            var Q576;
            Q576=makeQuery(id+"F11.opPattern","COPY",BODY,{"derivedFrom":makeQuery(id+"F10.opPattern","COPY",BODY,{"derivedFrom":makeQuery(id+"F1.opRevolve","SWEPT_BODY",BODY,{"disambiguationData":[OSD([sQuery(id+"F0.wireOp",EDGE,"E1")])]}),"instanceName":"1"}),"instanceName":"1"});
            var Q577;
            Q577=makeQuery(id+"F11.opPattern","COPY",BODY,{"derivedFrom":makeQuery(id+"F10.opPattern","COPY",BODY,{"derivedFrom":makeQuery(id+"F2.opPattern","COPY",BODY,{"derivedFrom":makeQuery(id+"F1.opRevolve","SWEPT_BODY",BODY,{"disambiguationData":[OSD([sQuery(id+"F0.wireOp",EDGE,"E1")])]}),"instanceName":"1"}),"instanceName":"1"}),"instanceName":"1"});
            var Q578;
            Q578=makeQuery(id+"F11.opPattern","COPY",BODY,{"derivedFrom":makeQuery(id+"F10.opPattern","COPY",BODY,{"derivedFrom":makeQuery(id+"F3.opPattern","COPY",BODY,{"derivedFrom":makeQuery(id+"F2.opPattern","COPY",BODY,{"derivedFrom":makeQuery(id+"F1.opRevolve","SWEPT_BODY",BODY,{"disambiguationData":[OSD([sQuery(id+"F0.wireOp",EDGE,"E1")])]}),"instanceName":"1"}),"instanceName":"1"}),"instanceName":"1"}),"instanceName":"1"});
            var Q579;
            Q579=makeQuery(id+"F11.opPattern","COPY",BODY,{"derivedFrom":makeQuery(id+"F10.opPattern","COPY",BODY,{"derivedFrom":makeQuery(id+"F4.opPattern","COPY",BODY,{"derivedFrom":makeQuery(id+"F1.opRevolve","SWEPT_BODY",BODY,{"disambiguationData":[OSD([sQuery(id+"F0.wireOp",EDGE,"E1")])]}),"instanceName":"1"}),"instanceName":"1"}),"instanceName":"1"});
            var Q580;
            Q580=makeQuery(id+"F11.opPattern","COPY",BODY,{"derivedFrom":makeQuery(id+"F10.opPattern","COPY",BODY,{"derivedFrom":makeQuery(id+"F4.opPattern","COPY",BODY,{"derivedFrom":makeQuery(id+"F2.opPattern","COPY",BODY,{"derivedFrom":makeQuery(id+"F1.opRevolve","SWEPT_BODY",BODY,{"disambiguationData":[OSD([sQuery(id+"F0.wireOp",EDGE,"E1")])]}),"instanceName":"1"}),"instanceName":"1"}),"instanceName":"1"}),"instanceName":"1"});
            var Q581;
            Q581=makeQuery(id+"F11.opPattern","COPY",BODY,{"derivedFrom":makeQuery(id+"F10.opPattern","COPY",BODY,{"derivedFrom":makeQuery(id+"F4.opPattern","COPY",BODY,{"derivedFrom":makeQuery(id+"F3.opPattern","COPY",BODY,{"derivedFrom":makeQuery(id+"F2.opPattern","COPY",BODY,{"derivedFrom":makeQuery(id+"F1.opRevolve","SWEPT_BODY",BODY,{"disambiguationData":[OSD([sQuery(id+"F0.wireOp",EDGE,"E1")])]}),"instanceName":"1"}),"instanceName":"1"}),"instanceName":"1"}),"instanceName":"1"}),"instanceName":"1"});
            var Q582;
            Q582=makeQuery(id+"F11.opPattern","COPY",BODY,{"derivedFrom":makeQuery(id+"F10.opPattern","COPY",BODY,{"derivedFrom":makeQuery(id+"F5.opPattern","COPY",BODY,{"derivedFrom":makeQuery(id+"F1.opRevolve","SWEPT_BODY",BODY,{"disambiguationData":[OSD([sQuery(id+"F0.wireOp",EDGE,"E1")])]}),"instanceName":"1"}),"instanceName":"1"}),"instanceName":"1"});
            var Q583;
            Q583=makeQuery(id+"F11.opPattern","COPY",BODY,{"derivedFrom":makeQuery(id+"F10.opPattern","COPY",BODY,{"derivedFrom":makeQuery(id+"F5.opPattern","COPY",BODY,{"derivedFrom":makeQuery(id+"F2.opPattern","COPY",BODY,{"derivedFrom":makeQuery(id+"F1.opRevolve","SWEPT_BODY",BODY,{"disambiguationData":[OSD([sQuery(id+"F0.wireOp",EDGE,"E1")])]}),"instanceName":"1"}),"instanceName":"1"}),"instanceName":"1"}),"instanceName":"1"});
            var Q584;
            Q584=makeQuery(id+"F11.opPattern","COPY",BODY,{"derivedFrom":makeQuery(id+"F10.opPattern","COPY",BODY,{"derivedFrom":makeQuery(id+"F5.opPattern","COPY",BODY,{"derivedFrom":makeQuery(id+"F3.opPattern","COPY",BODY,{"derivedFrom":makeQuery(id+"F2.opPattern","COPY",BODY,{"derivedFrom":makeQuery(id+"F1.opRevolve","SWEPT_BODY",BODY,{"disambiguationData":[OSD([sQuery(id+"F0.wireOp",EDGE,"E1")])]}),"instanceName":"1"}),"instanceName":"1"}),"instanceName":"1"}),"instanceName":"1"}),"instanceName":"1"});
            var Q585;
            Q585=makeQuery(id+"F11.opPattern","COPY",BODY,{"derivedFrom":makeQuery(id+"F10.opPattern","COPY",BODY,{"derivedFrom":makeQuery(id+"F5.opPattern","COPY",BODY,{"derivedFrom":makeQuery(id+"F4.opPattern","COPY",BODY,{"derivedFrom":makeQuery(id+"F1.opRevolve","SWEPT_BODY",BODY,{"disambiguationData":[OSD([sQuery(id+"F0.wireOp",EDGE,"E1")])]}),"instanceName":"1"}),"instanceName":"1"}),"instanceName":"1"}),"instanceName":"1"});
            var Q586;
            Q586=makeQuery(id+"F11.opPattern","COPY",BODY,{"derivedFrom":makeQuery(id+"F10.opPattern","COPY",BODY,{"derivedFrom":makeQuery(id+"F5.opPattern","COPY",BODY,{"derivedFrom":makeQuery(id+"F4.opPattern","COPY",BODY,{"derivedFrom":makeQuery(id+"F2.opPattern","COPY",BODY,{"derivedFrom":makeQuery(id+"F1.opRevolve","SWEPT_BODY",BODY,{"disambiguationData":[OSD([sQuery(id+"F0.wireOp",EDGE,"E1")])]}),"instanceName":"1"}),"instanceName":"1"}),"instanceName":"1"}),"instanceName":"1"}),"instanceName":"1"});
            var Q587;
            Q587=makeQuery(id+"F11.opPattern","COPY",BODY,{"derivedFrom":makeQuery(id+"F10.opPattern","COPY",BODY,{"derivedFrom":makeQuery(id+"F5.opPattern","COPY",BODY,{"derivedFrom":makeQuery(id+"F4.opPattern","COPY",BODY,{"derivedFrom":makeQuery(id+"F3.opPattern","COPY",BODY,{"derivedFrom":makeQuery(id+"F2.opPattern","COPY",BODY,{"derivedFrom":makeQuery(id+"F1.opRevolve","SWEPT_BODY",BODY,{"disambiguationData":[OSD([sQuery(id+"F0.wireOp",EDGE,"E1")])]}),"instanceName":"1"}),"instanceName":"1"}),"instanceName":"1"}),"instanceName":"1"}),"instanceName":"1"}),"instanceName":"1"});
            var Q588;
            Q588=makeQuery(id+"F11.opPattern","COPY",BODY,{"derivedFrom":makeQuery(id+"F10.opPattern","COPY",BODY,{"derivedFrom":makeQuery(id+"F6.opPattern","COPY",BODY,{"derivedFrom":makeQuery(id+"F1.opRevolve","SWEPT_BODY",BODY,{"disambiguationData":[OSD([sQuery(id+"F0.wireOp",EDGE,"E1")])]}),"instanceName":"1"}),"instanceName":"1"}),"instanceName":"1"});
            var Q589;
            Q589=makeQuery(id+"F11.opPattern","COPY",BODY,{"derivedFrom":makeQuery(id+"F10.opPattern","COPY",BODY,{"derivedFrom":makeQuery(id+"F6.opPattern","COPY",BODY,{"derivedFrom":makeQuery(id+"F2.opPattern","COPY",BODY,{"derivedFrom":makeQuery(id+"F1.opRevolve","SWEPT_BODY",BODY,{"disambiguationData":[OSD([sQuery(id+"F0.wireOp",EDGE,"E1")])]}),"instanceName":"1"}),"instanceName":"1"}),"instanceName":"1"}),"instanceName":"1"});
            var Q590;
            Q590=makeQuery(id+"F11.opPattern","COPY",BODY,{"derivedFrom":makeQuery(id+"F10.opPattern","COPY",BODY,{"derivedFrom":makeQuery(id+"F6.opPattern","COPY",BODY,{"derivedFrom":makeQuery(id+"F3.opPattern","COPY",BODY,{"derivedFrom":makeQuery(id+"F2.opPattern","COPY",BODY,{"derivedFrom":makeQuery(id+"F1.opRevolve","SWEPT_BODY",BODY,{"disambiguationData":[OSD([sQuery(id+"F0.wireOp",EDGE,"E1")])]}),"instanceName":"1"}),"instanceName":"1"}),"instanceName":"1"}),"instanceName":"1"}),"instanceName":"1"});
            var Q591;
            Q591=makeQuery(id+"F11.opPattern","COPY",BODY,{"derivedFrom":makeQuery(id+"F10.opPattern","COPY",BODY,{"derivedFrom":makeQuery(id+"F6.opPattern","COPY",BODY,{"derivedFrom":makeQuery(id+"F4.opPattern","COPY",BODY,{"derivedFrom":makeQuery(id+"F1.opRevolve","SWEPT_BODY",BODY,{"disambiguationData":[OSD([sQuery(id+"F0.wireOp",EDGE,"E1")])]}),"instanceName":"1"}),"instanceName":"1"}),"instanceName":"1"}),"instanceName":"1"});
            var Q592;
            Q592=makeQuery(id+"F11.opPattern","COPY",BODY,{"derivedFrom":makeQuery(id+"F10.opPattern","COPY",BODY,{"derivedFrom":makeQuery(id+"F6.opPattern","COPY",BODY,{"derivedFrom":makeQuery(id+"F4.opPattern","COPY",BODY,{"derivedFrom":makeQuery(id+"F2.opPattern","COPY",BODY,{"derivedFrom":makeQuery(id+"F1.opRevolve","SWEPT_BODY",BODY,{"disambiguationData":[OSD([sQuery(id+"F0.wireOp",EDGE,"E1")])]}),"instanceName":"1"}),"instanceName":"1"}),"instanceName":"1"}),"instanceName":"1"}),"instanceName":"1"});
            var Q593;
            Q593=makeQuery(id+"F11.opPattern","COPY",BODY,{"derivedFrom":makeQuery(id+"F10.opPattern","COPY",BODY,{"derivedFrom":makeQuery(id+"F6.opPattern","COPY",BODY,{"derivedFrom":makeQuery(id+"F4.opPattern","COPY",BODY,{"derivedFrom":makeQuery(id+"F3.opPattern","COPY",BODY,{"derivedFrom":makeQuery(id+"F2.opPattern","COPY",BODY,{"derivedFrom":makeQuery(id+"F1.opRevolve","SWEPT_BODY",BODY,{"disambiguationData":[OSD([sQuery(id+"F0.wireOp",EDGE,"E1")])]}),"instanceName":"1"}),"instanceName":"1"}),"instanceName":"1"}),"instanceName":"1"}),"instanceName":"1"}),"instanceName":"1"});
            var Q594;
            Q594=makeQuery(id+"F11.opPattern","COPY",BODY,{"derivedFrom":makeQuery(id+"F10.opPattern","COPY",BODY,{"derivedFrom":makeQuery(id+"F6.opPattern","COPY",BODY,{"derivedFrom":makeQuery(id+"F5.opPattern","COPY",BODY,{"derivedFrom":makeQuery(id+"F1.opRevolve","SWEPT_BODY",BODY,{"disambiguationData":[OSD([sQuery(id+"F0.wireOp",EDGE,"E1")])]}),"instanceName":"1"}),"instanceName":"1"}),"instanceName":"1"}),"instanceName":"1"});
            var Q595;
            Q595=makeQuery(id+"F11.opPattern","COPY",BODY,{"derivedFrom":makeQuery(id+"F10.opPattern","COPY",BODY,{"derivedFrom":makeQuery(id+"F6.opPattern","COPY",BODY,{"derivedFrom":makeQuery(id+"F5.opPattern","COPY",BODY,{"derivedFrom":makeQuery(id+"F2.opPattern","COPY",BODY,{"derivedFrom":makeQuery(id+"F1.opRevolve","SWEPT_BODY",BODY,{"disambiguationData":[OSD([sQuery(id+"F0.wireOp",EDGE,"E1")])]}),"instanceName":"1"}),"instanceName":"1"}),"instanceName":"1"}),"instanceName":"1"}),"instanceName":"1"});
            var Q596;
            Q596=makeQuery(id+"F11.opPattern","COPY",BODY,{"derivedFrom":makeQuery(id+"F10.opPattern","COPY",BODY,{"derivedFrom":makeQuery(id+"F6.opPattern","COPY",BODY,{"derivedFrom":makeQuery(id+"F5.opPattern","COPY",BODY,{"derivedFrom":makeQuery(id+"F3.opPattern","COPY",BODY,{"derivedFrom":makeQuery(id+"F2.opPattern","COPY",BODY,{"derivedFrom":makeQuery(id+"F1.opRevolve","SWEPT_BODY",BODY,{"disambiguationData":[OSD([sQuery(id+"F0.wireOp",EDGE,"E1")])]}),"instanceName":"1"}),"instanceName":"1"}),"instanceName":"1"}),"instanceName":"1"}),"instanceName":"1"}),"instanceName":"1"});
            var Q597;
            Q597=makeQuery(id+"F11.opPattern","COPY",BODY,{"derivedFrom":makeQuery(id+"F10.opPattern","COPY",BODY,{"derivedFrom":makeQuery(id+"F6.opPattern","COPY",BODY,{"derivedFrom":makeQuery(id+"F5.opPattern","COPY",BODY,{"derivedFrom":makeQuery(id+"F4.opPattern","COPY",BODY,{"derivedFrom":makeQuery(id+"F1.opRevolve","SWEPT_BODY",BODY,{"disambiguationData":[OSD([sQuery(id+"F0.wireOp",EDGE,"E1")])]}),"instanceName":"1"}),"instanceName":"1"}),"instanceName":"1"}),"instanceName":"1"}),"instanceName":"1"});
            var Q598;
            Q598=makeQuery(id+"F11.opPattern","COPY",BODY,{"derivedFrom":makeQuery(id+"F10.opPattern","COPY",BODY,{"derivedFrom":makeQuery(id+"F6.opPattern","COPY",BODY,{"derivedFrom":makeQuery(id+"F5.opPattern","COPY",BODY,{"derivedFrom":makeQuery(id+"F4.opPattern","COPY",BODY,{"derivedFrom":makeQuery(id+"F2.opPattern","COPY",BODY,{"derivedFrom":makeQuery(id+"F1.opRevolve","SWEPT_BODY",BODY,{"disambiguationData":[OSD([sQuery(id+"F0.wireOp",EDGE,"E1")])]}),"instanceName":"1"}),"instanceName":"1"}),"instanceName":"1"}),"instanceName":"1"}),"instanceName":"1"}),"instanceName":"1"});
            var Q599;
            Q599=makeQuery(id+"F11.opPattern","COPY",BODY,{"derivedFrom":makeQuery(id+"F10.opPattern","COPY",BODY,{"derivedFrom":makeQuery(id+"F6.opPattern","COPY",BODY,{"derivedFrom":makeQuery(id+"F5.opPattern","COPY",BODY,{"derivedFrom":makeQuery(id+"F4.opPattern","COPY",BODY,{"derivedFrom":makeQuery(id+"F3.opPattern","COPY",BODY,{"derivedFrom":makeQuery(id+"F2.opPattern","COPY",BODY,{"derivedFrom":makeQuery(id+"F1.opRevolve","SWEPT_BODY",BODY,{"disambiguationData":[OSD([sQuery(id+"F0.wireOp",EDGE,"E1")])]}),"instanceName":"1"}),"instanceName":"1"}),"instanceName":"1"}),"instanceName":"1"}),"instanceName":"1"}),"instanceName":"1"}),"instanceName":"1"});
            var Q600;
            Q600=makeQuery(id+"F11.opPattern","COPY",BODY,{"derivedFrom":makeQuery(id+"F10.opPattern","COPY",BODY,{"derivedFrom":makeQuery(id+"F7.opPattern","COPY",BODY,{"derivedFrom":makeQuery(id+"F1.opRevolve","SWEPT_BODY",BODY,{"disambiguationData":[OSD([sQuery(id+"F0.wireOp",EDGE,"E1")])]}),"instanceName":"1"}),"instanceName":"1"}),"instanceName":"1"});
            var Q601;
            Q601=makeQuery(id+"F11.opPattern","COPY",BODY,{"derivedFrom":makeQuery(id+"F10.opPattern","COPY",BODY,{"derivedFrom":makeQuery(id+"F7.opPattern","COPY",BODY,{"derivedFrom":makeQuery(id+"F2.opPattern","COPY",BODY,{"derivedFrom":makeQuery(id+"F1.opRevolve","SWEPT_BODY",BODY,{"disambiguationData":[OSD([sQuery(id+"F0.wireOp",EDGE,"E1")])]}),"instanceName":"1"}),"instanceName":"1"}),"instanceName":"1"}),"instanceName":"1"});
            var Q602;
            Q602=makeQuery(id+"F11.opPattern","COPY",BODY,{"derivedFrom":makeQuery(id+"F10.opPattern","COPY",BODY,{"derivedFrom":makeQuery(id+"F7.opPattern","COPY",BODY,{"derivedFrom":makeQuery(id+"F3.opPattern","COPY",BODY,{"derivedFrom":makeQuery(id+"F2.opPattern","COPY",BODY,{"derivedFrom":makeQuery(id+"F1.opRevolve","SWEPT_BODY",BODY,{"disambiguationData":[OSD([sQuery(id+"F0.wireOp",EDGE,"E1")])]}),"instanceName":"1"}),"instanceName":"1"}),"instanceName":"1"}),"instanceName":"1"}),"instanceName":"1"});
            var Q603;
            Q603=makeQuery(id+"F11.opPattern","COPY",BODY,{"derivedFrom":makeQuery(id+"F10.opPattern","COPY",BODY,{"derivedFrom":makeQuery(id+"F7.opPattern","COPY",BODY,{"derivedFrom":makeQuery(id+"F4.opPattern","COPY",BODY,{"derivedFrom":makeQuery(id+"F1.opRevolve","SWEPT_BODY",BODY,{"disambiguationData":[OSD([sQuery(id+"F0.wireOp",EDGE,"E1")])]}),"instanceName":"1"}),"instanceName":"1"}),"instanceName":"1"}),"instanceName":"1"});
            var Q604;
            Q604=makeQuery(id+"F11.opPattern","COPY",BODY,{"derivedFrom":makeQuery(id+"F10.opPattern","COPY",BODY,{"derivedFrom":makeQuery(id+"F7.opPattern","COPY",BODY,{"derivedFrom":makeQuery(id+"F4.opPattern","COPY",BODY,{"derivedFrom":makeQuery(id+"F2.opPattern","COPY",BODY,{"derivedFrom":makeQuery(id+"F1.opRevolve","SWEPT_BODY",BODY,{"disambiguationData":[OSD([sQuery(id+"F0.wireOp",EDGE,"E1")])]}),"instanceName":"1"}),"instanceName":"1"}),"instanceName":"1"}),"instanceName":"1"}),"instanceName":"1"});
            var Q605;
            Q605=makeQuery(id+"F11.opPattern","COPY",BODY,{"derivedFrom":makeQuery(id+"F10.opPattern","COPY",BODY,{"derivedFrom":makeQuery(id+"F7.opPattern","COPY",BODY,{"derivedFrom":makeQuery(id+"F4.opPattern","COPY",BODY,{"derivedFrom":makeQuery(id+"F3.opPattern","COPY",BODY,{"derivedFrom":makeQuery(id+"F2.opPattern","COPY",BODY,{"derivedFrom":makeQuery(id+"F1.opRevolve","SWEPT_BODY",BODY,{"disambiguationData":[OSD([sQuery(id+"F0.wireOp",EDGE,"E1")])]}),"instanceName":"1"}),"instanceName":"1"}),"instanceName":"1"}),"instanceName":"1"}),"instanceName":"1"}),"instanceName":"1"});
            var Q606;
            Q606=makeQuery(id+"F11.opPattern","COPY",BODY,{"derivedFrom":makeQuery(id+"F10.opPattern","COPY",BODY,{"derivedFrom":makeQuery(id+"F7.opPattern","COPY",BODY,{"derivedFrom":makeQuery(id+"F5.opPattern","COPY",BODY,{"derivedFrom":makeQuery(id+"F1.opRevolve","SWEPT_BODY",BODY,{"disambiguationData":[OSD([sQuery(id+"F0.wireOp",EDGE,"E1")])]}),"instanceName":"1"}),"instanceName":"1"}),"instanceName":"1"}),"instanceName":"1"});
            var Q607;
            Q607=makeQuery(id+"F11.opPattern","COPY",BODY,{"derivedFrom":makeQuery(id+"F10.opPattern","COPY",BODY,{"derivedFrom":makeQuery(id+"F7.opPattern","COPY",BODY,{"derivedFrom":makeQuery(id+"F5.opPattern","COPY",BODY,{"derivedFrom":makeQuery(id+"F2.opPattern","COPY",BODY,{"derivedFrom":makeQuery(id+"F1.opRevolve","SWEPT_BODY",BODY,{"disambiguationData":[OSD([sQuery(id+"F0.wireOp",EDGE,"E1")])]}),"instanceName":"1"}),"instanceName":"1"}),"instanceName":"1"}),"instanceName":"1"}),"instanceName":"1"});
            var Q608;
            Q608=makeQuery(id+"F11.opPattern","COPY",BODY,{"derivedFrom":makeQuery(id+"F10.opPattern","COPY",BODY,{"derivedFrom":makeQuery(id+"F7.opPattern","COPY",BODY,{"derivedFrom":makeQuery(id+"F5.opPattern","COPY",BODY,{"derivedFrom":makeQuery(id+"F3.opPattern","COPY",BODY,{"derivedFrom":makeQuery(id+"F2.opPattern","COPY",BODY,{"derivedFrom":makeQuery(id+"F1.opRevolve","SWEPT_BODY",BODY,{"disambiguationData":[OSD([sQuery(id+"F0.wireOp",EDGE,"E1")])]}),"instanceName":"1"}),"instanceName":"1"}),"instanceName":"1"}),"instanceName":"1"}),"instanceName":"1"}),"instanceName":"1"});
            var Q609;
            Q609=makeQuery(id+"F11.opPattern","COPY",BODY,{"derivedFrom":makeQuery(id+"F10.opPattern","COPY",BODY,{"derivedFrom":makeQuery(id+"F7.opPattern","COPY",BODY,{"derivedFrom":makeQuery(id+"F5.opPattern","COPY",BODY,{"derivedFrom":makeQuery(id+"F4.opPattern","COPY",BODY,{"derivedFrom":makeQuery(id+"F1.opRevolve","SWEPT_BODY",BODY,{"disambiguationData":[OSD([sQuery(id+"F0.wireOp",EDGE,"E1")])]}),"instanceName":"1"}),"instanceName":"1"}),"instanceName":"1"}),"instanceName":"1"}),"instanceName":"1"});
            var Q610;
            Q610=makeQuery(id+"F11.opPattern","COPY",BODY,{"derivedFrom":makeQuery(id+"F10.opPattern","COPY",BODY,{"derivedFrom":makeQuery(id+"F7.opPattern","COPY",BODY,{"derivedFrom":makeQuery(id+"F5.opPattern","COPY",BODY,{"derivedFrom":makeQuery(id+"F4.opPattern","COPY",BODY,{"derivedFrom":makeQuery(id+"F2.opPattern","COPY",BODY,{"derivedFrom":makeQuery(id+"F1.opRevolve","SWEPT_BODY",BODY,{"disambiguationData":[OSD([sQuery(id+"F0.wireOp",EDGE,"E1")])]}),"instanceName":"1"}),"instanceName":"1"}),"instanceName":"1"}),"instanceName":"1"}),"instanceName":"1"}),"instanceName":"1"});
            var Q611;
            Q611=makeQuery(id+"F11.opPattern","COPY",BODY,{"derivedFrom":makeQuery(id+"F10.opPattern","COPY",BODY,{"derivedFrom":makeQuery(id+"F7.opPattern","COPY",BODY,{"derivedFrom":makeQuery(id+"F5.opPattern","COPY",BODY,{"derivedFrom":makeQuery(id+"F4.opPattern","COPY",BODY,{"derivedFrom":makeQuery(id+"F3.opPattern","COPY",BODY,{"derivedFrom":makeQuery(id+"F2.opPattern","COPY",BODY,{"derivedFrom":makeQuery(id+"F1.opRevolve","SWEPT_BODY",BODY,{"disambiguationData":[OSD([sQuery(id+"F0.wireOp",EDGE,"E1")])]}),"instanceName":"1"}),"instanceName":"1"}),"instanceName":"1"}),"instanceName":"1"}),"instanceName":"1"}),"instanceName":"1"}),"instanceName":"1"});
            var Q612;
            Q612=makeQuery(id+"F11.opPattern","COPY",BODY,{"derivedFrom":makeQuery(id+"F10.opPattern","COPY",BODY,{"derivedFrom":makeQuery(id+"F7.opPattern","COPY",BODY,{"derivedFrom":makeQuery(id+"F6.opPattern","COPY",BODY,{"derivedFrom":makeQuery(id+"F1.opRevolve","SWEPT_BODY",BODY,{"disambiguationData":[OSD([sQuery(id+"F0.wireOp",EDGE,"E1")])]}),"instanceName":"1"}),"instanceName":"1"}),"instanceName":"1"}),"instanceName":"1"});
            var Q613;
            Q613=makeQuery(id+"F11.opPattern","COPY",BODY,{"derivedFrom":makeQuery(id+"F10.opPattern","COPY",BODY,{"derivedFrom":makeQuery(id+"F7.opPattern","COPY",BODY,{"derivedFrom":makeQuery(id+"F6.opPattern","COPY",BODY,{"derivedFrom":makeQuery(id+"F2.opPattern","COPY",BODY,{"derivedFrom":makeQuery(id+"F1.opRevolve","SWEPT_BODY",BODY,{"disambiguationData":[OSD([sQuery(id+"F0.wireOp",EDGE,"E1")])]}),"instanceName":"1"}),"instanceName":"1"}),"instanceName":"1"}),"instanceName":"1"}),"instanceName":"1"});
            var Q614;
            Q614=makeQuery(id+"F11.opPattern","COPY",BODY,{"derivedFrom":makeQuery(id+"F10.opPattern","COPY",BODY,{"derivedFrom":makeQuery(id+"F7.opPattern","COPY",BODY,{"derivedFrom":makeQuery(id+"F6.opPattern","COPY",BODY,{"derivedFrom":makeQuery(id+"F3.opPattern","COPY",BODY,{"derivedFrom":makeQuery(id+"F2.opPattern","COPY",BODY,{"derivedFrom":makeQuery(id+"F1.opRevolve","SWEPT_BODY",BODY,{"disambiguationData":[OSD([sQuery(id+"F0.wireOp",EDGE,"E1")])]}),"instanceName":"1"}),"instanceName":"1"}),"instanceName":"1"}),"instanceName":"1"}),"instanceName":"1"}),"instanceName":"1"});
            var Q615;
            Q615=makeQuery(id+"F11.opPattern","COPY",BODY,{"derivedFrom":makeQuery(id+"F10.opPattern","COPY",BODY,{"derivedFrom":makeQuery(id+"F7.opPattern","COPY",BODY,{"derivedFrom":makeQuery(id+"F6.opPattern","COPY",BODY,{"derivedFrom":makeQuery(id+"F4.opPattern","COPY",BODY,{"derivedFrom":makeQuery(id+"F1.opRevolve","SWEPT_BODY",BODY,{"disambiguationData":[OSD([sQuery(id+"F0.wireOp",EDGE,"E1")])]}),"instanceName":"1"}),"instanceName":"1"}),"instanceName":"1"}),"instanceName":"1"}),"instanceName":"1"});
            var Q616;
            Q616=makeQuery(id+"F11.opPattern","COPY",BODY,{"derivedFrom":makeQuery(id+"F10.opPattern","COPY",BODY,{"derivedFrom":makeQuery(id+"F7.opPattern","COPY",BODY,{"derivedFrom":makeQuery(id+"F6.opPattern","COPY",BODY,{"derivedFrom":makeQuery(id+"F4.opPattern","COPY",BODY,{"derivedFrom":makeQuery(id+"F2.opPattern","COPY",BODY,{"derivedFrom":makeQuery(id+"F1.opRevolve","SWEPT_BODY",BODY,{"disambiguationData":[OSD([sQuery(id+"F0.wireOp",EDGE,"E1")])]}),"instanceName":"1"}),"instanceName":"1"}),"instanceName":"1"}),"instanceName":"1"}),"instanceName":"1"}),"instanceName":"1"});
            var Q617;
            Q617=makeQuery(id+"F11.opPattern","COPY",BODY,{"derivedFrom":makeQuery(id+"F10.opPattern","COPY",BODY,{"derivedFrom":makeQuery(id+"F7.opPattern","COPY",BODY,{"derivedFrom":makeQuery(id+"F6.opPattern","COPY",BODY,{"derivedFrom":makeQuery(id+"F4.opPattern","COPY",BODY,{"derivedFrom":makeQuery(id+"F3.opPattern","COPY",BODY,{"derivedFrom":makeQuery(id+"F2.opPattern","COPY",BODY,{"derivedFrom":makeQuery(id+"F1.opRevolve","SWEPT_BODY",BODY,{"disambiguationData":[OSD([sQuery(id+"F0.wireOp",EDGE,"E1")])]}),"instanceName":"1"}),"instanceName":"1"}),"instanceName":"1"}),"instanceName":"1"}),"instanceName":"1"}),"instanceName":"1"}),"instanceName":"1"});
            var Q618;
            Q618=makeQuery(id+"F11.opPattern","COPY",BODY,{"derivedFrom":makeQuery(id+"F10.opPattern","COPY",BODY,{"derivedFrom":makeQuery(id+"F7.opPattern","COPY",BODY,{"derivedFrom":makeQuery(id+"F6.opPattern","COPY",BODY,{"derivedFrom":makeQuery(id+"F5.opPattern","COPY",BODY,{"derivedFrom":makeQuery(id+"F1.opRevolve","SWEPT_BODY",BODY,{"disambiguationData":[OSD([sQuery(id+"F0.wireOp",EDGE,"E1")])]}),"instanceName":"1"}),"instanceName":"1"}),"instanceName":"1"}),"instanceName":"1"}),"instanceName":"1"});
            var Q619;
            Q619=makeQuery(id+"F11.opPattern","COPY",BODY,{"derivedFrom":makeQuery(id+"F10.opPattern","COPY",BODY,{"derivedFrom":makeQuery(id+"F7.opPattern","COPY",BODY,{"derivedFrom":makeQuery(id+"F6.opPattern","COPY",BODY,{"derivedFrom":makeQuery(id+"F5.opPattern","COPY",BODY,{"derivedFrom":makeQuery(id+"F2.opPattern","COPY",BODY,{"derivedFrom":makeQuery(id+"F1.opRevolve","SWEPT_BODY",BODY,{"disambiguationData":[OSD([sQuery(id+"F0.wireOp",EDGE,"E1")])]}),"instanceName":"1"}),"instanceName":"1"}),"instanceName":"1"}),"instanceName":"1"}),"instanceName":"1"}),"instanceName":"1"});
            var Q620;
            Q620=makeQuery(id+"F11.opPattern","COPY",BODY,{"derivedFrom":makeQuery(id+"F10.opPattern","COPY",BODY,{"derivedFrom":makeQuery(id+"F7.opPattern","COPY",BODY,{"derivedFrom":makeQuery(id+"F6.opPattern","COPY",BODY,{"derivedFrom":makeQuery(id+"F5.opPattern","COPY",BODY,{"derivedFrom":makeQuery(id+"F3.opPattern","COPY",BODY,{"derivedFrom":makeQuery(id+"F2.opPattern","COPY",BODY,{"derivedFrom":makeQuery(id+"F1.opRevolve","SWEPT_BODY",BODY,{"disambiguationData":[OSD([sQuery(id+"F0.wireOp",EDGE,"E1")])]}),"instanceName":"1"}),"instanceName":"1"}),"instanceName":"1"}),"instanceName":"1"}),"instanceName":"1"}),"instanceName":"1"}),"instanceName":"1"});
            var Q621;
            Q621=makeQuery(id+"F11.opPattern","COPY",BODY,{"derivedFrom":makeQuery(id+"F10.opPattern","COPY",BODY,{"derivedFrom":makeQuery(id+"F7.opPattern","COPY",BODY,{"derivedFrom":makeQuery(id+"F6.opPattern","COPY",BODY,{"derivedFrom":makeQuery(id+"F5.opPattern","COPY",BODY,{"derivedFrom":makeQuery(id+"F4.opPattern","COPY",BODY,{"derivedFrom":makeQuery(id+"F1.opRevolve","SWEPT_BODY",BODY,{"disambiguationData":[OSD([sQuery(id+"F0.wireOp",EDGE,"E1")])]}),"instanceName":"1"}),"instanceName":"1"}),"instanceName":"1"}),"instanceName":"1"}),"instanceName":"1"}),"instanceName":"1"});
            var Q622;
            Q622=makeQuery(id+"F11.opPattern","COPY",BODY,{"derivedFrom":makeQuery(id+"F10.opPattern","COPY",BODY,{"derivedFrom":makeQuery(id+"F7.opPattern","COPY",BODY,{"derivedFrom":makeQuery(id+"F6.opPattern","COPY",BODY,{"derivedFrom":makeQuery(id+"F5.opPattern","COPY",BODY,{"derivedFrom":makeQuery(id+"F4.opPattern","COPY",BODY,{"derivedFrom":makeQuery(id+"F2.opPattern","COPY",BODY,{"derivedFrom":makeQuery(id+"F1.opRevolve","SWEPT_BODY",BODY,{"disambiguationData":[OSD([sQuery(id+"F0.wireOp",EDGE,"E1")])]}),"instanceName":"1"}),"instanceName":"1"}),"instanceName":"1"}),"instanceName":"1"}),"instanceName":"1"}),"instanceName":"1"}),"instanceName":"1"});
            var Q623;
            Q623=makeQuery(id+"F11.opPattern","COPY",BODY,{"derivedFrom":makeQuery(id+"F10.opPattern","COPY",BODY,{"derivedFrom":makeQuery(id+"F7.opPattern","COPY",BODY,{"derivedFrom":makeQuery(id+"F6.opPattern","COPY",BODY,{"derivedFrom":makeQuery(id+"F5.opPattern","COPY",BODY,{"derivedFrom":makeQuery(id+"F4.opPattern","COPY",BODY,{"derivedFrom":makeQuery(id+"F3.opPattern","COPY",BODY,{"derivedFrom":makeQuery(id+"F2.opPattern","COPY",BODY,{"derivedFrom":makeQuery(id+"F1.opRevolve","SWEPT_BODY",BODY,{"disambiguationData":[OSD([sQuery(id+"F0.wireOp",EDGE,"E1")])]}),"instanceName":"1"}),"instanceName":"1"}),"instanceName":"1"}),"instanceName":"1"}),"instanceName":"1"}),"instanceName":"1"}),"instanceName":"1"}),"instanceName":"1"});
            var Q624;
            Q624=makeQuery(id+"F11.opPattern","COPY",BODY,{"derivedFrom":makeQuery(id+"F10.opPattern","COPY",BODY,{"derivedFrom":makeQuery(id+"F8.opPattern","COPY",BODY,{"derivedFrom":makeQuery(id+"F1.opRevolve","SWEPT_BODY",BODY,{"disambiguationData":[OSD([sQuery(id+"F0.wireOp",EDGE,"E1")])]}),"instanceName":"1"}),"instanceName":"1"}),"instanceName":"1"});
            var Q625;
            Q625=makeQuery(id+"F11.opPattern","COPY",BODY,{"derivedFrom":makeQuery(id+"F10.opPattern","COPY",BODY,{"derivedFrom":makeQuery(id+"F8.opPattern","COPY",BODY,{"derivedFrom":makeQuery(id+"F2.opPattern","COPY",BODY,{"derivedFrom":makeQuery(id+"F1.opRevolve","SWEPT_BODY",BODY,{"disambiguationData":[OSD([sQuery(id+"F0.wireOp",EDGE,"E1")])]}),"instanceName":"1"}),"instanceName":"1"}),"instanceName":"1"}),"instanceName":"1"});
            var Q626;
            Q626=makeQuery(id+"F11.opPattern","COPY",BODY,{"derivedFrom":makeQuery(id+"F10.opPattern","COPY",BODY,{"derivedFrom":makeQuery(id+"F8.opPattern","COPY",BODY,{"derivedFrom":makeQuery(id+"F3.opPattern","COPY",BODY,{"derivedFrom":makeQuery(id+"F2.opPattern","COPY",BODY,{"derivedFrom":makeQuery(id+"F1.opRevolve","SWEPT_BODY",BODY,{"disambiguationData":[OSD([sQuery(id+"F0.wireOp",EDGE,"E1")])]}),"instanceName":"1"}),"instanceName":"1"}),"instanceName":"1"}),"instanceName":"1"}),"instanceName":"1"});
            var Q627;
            Q627=makeQuery(id+"F11.opPattern","COPY",BODY,{"derivedFrom":makeQuery(id+"F10.opPattern","COPY",BODY,{"derivedFrom":makeQuery(id+"F8.opPattern","COPY",BODY,{"derivedFrom":makeQuery(id+"F4.opPattern","COPY",BODY,{"derivedFrom":makeQuery(id+"F1.opRevolve","SWEPT_BODY",BODY,{"disambiguationData":[OSD([sQuery(id+"F0.wireOp",EDGE,"E1")])]}),"instanceName":"1"}),"instanceName":"1"}),"instanceName":"1"}),"instanceName":"1"});
            var Q628;
            Q628=makeQuery(id+"F11.opPattern","COPY",BODY,{"derivedFrom":makeQuery(id+"F10.opPattern","COPY",BODY,{"derivedFrom":makeQuery(id+"F8.opPattern","COPY",BODY,{"derivedFrom":makeQuery(id+"F4.opPattern","COPY",BODY,{"derivedFrom":makeQuery(id+"F2.opPattern","COPY",BODY,{"derivedFrom":makeQuery(id+"F1.opRevolve","SWEPT_BODY",BODY,{"disambiguationData":[OSD([sQuery(id+"F0.wireOp",EDGE,"E1")])]}),"instanceName":"1"}),"instanceName":"1"}),"instanceName":"1"}),"instanceName":"1"}),"instanceName":"1"});
            var Q629;
            Q629=makeQuery(id+"F11.opPattern","COPY",BODY,{"derivedFrom":makeQuery(id+"F10.opPattern","COPY",BODY,{"derivedFrom":makeQuery(id+"F8.opPattern","COPY",BODY,{"derivedFrom":makeQuery(id+"F4.opPattern","COPY",BODY,{"derivedFrom":makeQuery(id+"F3.opPattern","COPY",BODY,{"derivedFrom":makeQuery(id+"F2.opPattern","COPY",BODY,{"derivedFrom":makeQuery(id+"F1.opRevolve","SWEPT_BODY",BODY,{"disambiguationData":[OSD([sQuery(id+"F0.wireOp",EDGE,"E1")])]}),"instanceName":"1"}),"instanceName":"1"}),"instanceName":"1"}),"instanceName":"1"}),"instanceName":"1"}),"instanceName":"1"});
            var Q630;
            Q630=makeQuery(id+"F11.opPattern","COPY",BODY,{"derivedFrom":makeQuery(id+"F10.opPattern","COPY",BODY,{"derivedFrom":makeQuery(id+"F8.opPattern","COPY",BODY,{"derivedFrom":makeQuery(id+"F5.opPattern","COPY",BODY,{"derivedFrom":makeQuery(id+"F1.opRevolve","SWEPT_BODY",BODY,{"disambiguationData":[OSD([sQuery(id+"F0.wireOp",EDGE,"E1")])]}),"instanceName":"1"}),"instanceName":"1"}),"instanceName":"1"}),"instanceName":"1"});
            var Q631;
            Q631=makeQuery(id+"F11.opPattern","COPY",BODY,{"derivedFrom":makeQuery(id+"F10.opPattern","COPY",BODY,{"derivedFrom":makeQuery(id+"F8.opPattern","COPY",BODY,{"derivedFrom":makeQuery(id+"F5.opPattern","COPY",BODY,{"derivedFrom":makeQuery(id+"F2.opPattern","COPY",BODY,{"derivedFrom":makeQuery(id+"F1.opRevolve","SWEPT_BODY",BODY,{"disambiguationData":[OSD([sQuery(id+"F0.wireOp",EDGE,"E1")])]}),"instanceName":"1"}),"instanceName":"1"}),"instanceName":"1"}),"instanceName":"1"}),"instanceName":"1"});
            var Q632;
            Q632=makeQuery(id+"F11.opPattern","COPY",BODY,{"derivedFrom":makeQuery(id+"F10.opPattern","COPY",BODY,{"derivedFrom":makeQuery(id+"F8.opPattern","COPY",BODY,{"derivedFrom":makeQuery(id+"F5.opPattern","COPY",BODY,{"derivedFrom":makeQuery(id+"F3.opPattern","COPY",BODY,{"derivedFrom":makeQuery(id+"F2.opPattern","COPY",BODY,{"derivedFrom":makeQuery(id+"F1.opRevolve","SWEPT_BODY",BODY,{"disambiguationData":[OSD([sQuery(id+"F0.wireOp",EDGE,"E1")])]}),"instanceName":"1"}),"instanceName":"1"}),"instanceName":"1"}),"instanceName":"1"}),"instanceName":"1"}),"instanceName":"1"});
            var Q633;
            Q633=makeQuery(id+"F11.opPattern","COPY",BODY,{"derivedFrom":makeQuery(id+"F10.opPattern","COPY",BODY,{"derivedFrom":makeQuery(id+"F8.opPattern","COPY",BODY,{"derivedFrom":makeQuery(id+"F5.opPattern","COPY",BODY,{"derivedFrom":makeQuery(id+"F4.opPattern","COPY",BODY,{"derivedFrom":makeQuery(id+"F1.opRevolve","SWEPT_BODY",BODY,{"disambiguationData":[OSD([sQuery(id+"F0.wireOp",EDGE,"E1")])]}),"instanceName":"1"}),"instanceName":"1"}),"instanceName":"1"}),"instanceName":"1"}),"instanceName":"1"});
            var Q634;
            Q634=makeQuery(id+"F11.opPattern","COPY",BODY,{"derivedFrom":makeQuery(id+"F10.opPattern","COPY",BODY,{"derivedFrom":makeQuery(id+"F8.opPattern","COPY",BODY,{"derivedFrom":makeQuery(id+"F5.opPattern","COPY",BODY,{"derivedFrom":makeQuery(id+"F4.opPattern","COPY",BODY,{"derivedFrom":makeQuery(id+"F2.opPattern","COPY",BODY,{"derivedFrom":makeQuery(id+"F1.opRevolve","SWEPT_BODY",BODY,{"disambiguationData":[OSD([sQuery(id+"F0.wireOp",EDGE,"E1")])]}),"instanceName":"1"}),"instanceName":"1"}),"instanceName":"1"}),"instanceName":"1"}),"instanceName":"1"}),"instanceName":"1"});
            var Q635;
            Q635=makeQuery(id+"F11.opPattern","COPY",BODY,{"derivedFrom":makeQuery(id+"F10.opPattern","COPY",BODY,{"derivedFrom":makeQuery(id+"F8.opPattern","COPY",BODY,{"derivedFrom":makeQuery(id+"F5.opPattern","COPY",BODY,{"derivedFrom":makeQuery(id+"F4.opPattern","COPY",BODY,{"derivedFrom":makeQuery(id+"F3.opPattern","COPY",BODY,{"derivedFrom":makeQuery(id+"F2.opPattern","COPY",BODY,{"derivedFrom":makeQuery(id+"F1.opRevolve","SWEPT_BODY",BODY,{"disambiguationData":[OSD([sQuery(id+"F0.wireOp",EDGE,"E1")])]}),"instanceName":"1"}),"instanceName":"1"}),"instanceName":"1"}),"instanceName":"1"}),"instanceName":"1"}),"instanceName":"1"}),"instanceName":"1"});
            var Q636;
            Q636=makeQuery(id+"F11.opPattern","COPY",BODY,{"derivedFrom":makeQuery(id+"F10.opPattern","COPY",BODY,{"derivedFrom":makeQuery(id+"F8.opPattern","COPY",BODY,{"derivedFrom":makeQuery(id+"F6.opPattern","COPY",BODY,{"derivedFrom":makeQuery(id+"F1.opRevolve","SWEPT_BODY",BODY,{"disambiguationData":[OSD([sQuery(id+"F0.wireOp",EDGE,"E1")])]}),"instanceName":"1"}),"instanceName":"1"}),"instanceName":"1"}),"instanceName":"1"});
            var Q637;
            Q637=makeQuery(id+"F11.opPattern","COPY",BODY,{"derivedFrom":makeQuery(id+"F10.opPattern","COPY",BODY,{"derivedFrom":makeQuery(id+"F8.opPattern","COPY",BODY,{"derivedFrom":makeQuery(id+"F6.opPattern","COPY",BODY,{"derivedFrom":makeQuery(id+"F2.opPattern","COPY",BODY,{"derivedFrom":makeQuery(id+"F1.opRevolve","SWEPT_BODY",BODY,{"disambiguationData":[OSD([sQuery(id+"F0.wireOp",EDGE,"E1")])]}),"instanceName":"1"}),"instanceName":"1"}),"instanceName":"1"}),"instanceName":"1"}),"instanceName":"1"});
            var Q638;
            Q638=makeQuery(id+"F11.opPattern","COPY",BODY,{"derivedFrom":makeQuery(id+"F10.opPattern","COPY",BODY,{"derivedFrom":makeQuery(id+"F8.opPattern","COPY",BODY,{"derivedFrom":makeQuery(id+"F6.opPattern","COPY",BODY,{"derivedFrom":makeQuery(id+"F3.opPattern","COPY",BODY,{"derivedFrom":makeQuery(id+"F2.opPattern","COPY",BODY,{"derivedFrom":makeQuery(id+"F1.opRevolve","SWEPT_BODY",BODY,{"disambiguationData":[OSD([sQuery(id+"F0.wireOp",EDGE,"E1")])]}),"instanceName":"1"}),"instanceName":"1"}),"instanceName":"1"}),"instanceName":"1"}),"instanceName":"1"}),"instanceName":"1"});
            var Q639;
            Q639=makeQuery(id+"F11.opPattern","COPY",BODY,{"derivedFrom":makeQuery(id+"F10.opPattern","COPY",BODY,{"derivedFrom":makeQuery(id+"F8.opPattern","COPY",BODY,{"derivedFrom":makeQuery(id+"F6.opPattern","COPY",BODY,{"derivedFrom":makeQuery(id+"F4.opPattern","COPY",BODY,{"derivedFrom":makeQuery(id+"F1.opRevolve","SWEPT_BODY",BODY,{"disambiguationData":[OSD([sQuery(id+"F0.wireOp",EDGE,"E1")])]}),"instanceName":"1"}),"instanceName":"1"}),"instanceName":"1"}),"instanceName":"1"}),"instanceName":"1"});
            var Q640;
            Q640=makeQuery(id+"F11.opPattern","COPY",BODY,{"derivedFrom":makeQuery(id+"F10.opPattern","COPY",BODY,{"derivedFrom":makeQuery(id+"F8.opPattern","COPY",BODY,{"derivedFrom":makeQuery(id+"F6.opPattern","COPY",BODY,{"derivedFrom":makeQuery(id+"F4.opPattern","COPY",BODY,{"derivedFrom":makeQuery(id+"F2.opPattern","COPY",BODY,{"derivedFrom":makeQuery(id+"F1.opRevolve","SWEPT_BODY",BODY,{"disambiguationData":[OSD([sQuery(id+"F0.wireOp",EDGE,"E1")])]}),"instanceName":"1"}),"instanceName":"1"}),"instanceName":"1"}),"instanceName":"1"}),"instanceName":"1"}),"instanceName":"1"});
            var Q641;
            Q641=makeQuery(id+"F11.opPattern","COPY",BODY,{"derivedFrom":makeQuery(id+"F10.opPattern","COPY",BODY,{"derivedFrom":makeQuery(id+"F8.opPattern","COPY",BODY,{"derivedFrom":makeQuery(id+"F6.opPattern","COPY",BODY,{"derivedFrom":makeQuery(id+"F4.opPattern","COPY",BODY,{"derivedFrom":makeQuery(id+"F3.opPattern","COPY",BODY,{"derivedFrom":makeQuery(id+"F2.opPattern","COPY",BODY,{"derivedFrom":makeQuery(id+"F1.opRevolve","SWEPT_BODY",BODY,{"disambiguationData":[OSD([sQuery(id+"F0.wireOp",EDGE,"E1")])]}),"instanceName":"1"}),"instanceName":"1"}),"instanceName":"1"}),"instanceName":"1"}),"instanceName":"1"}),"instanceName":"1"}),"instanceName":"1"});
            var Q642;
            Q642=makeQuery(id+"F11.opPattern","COPY",BODY,{"derivedFrom":makeQuery(id+"F10.opPattern","COPY",BODY,{"derivedFrom":makeQuery(id+"F8.opPattern","COPY",BODY,{"derivedFrom":makeQuery(id+"F6.opPattern","COPY",BODY,{"derivedFrom":makeQuery(id+"F5.opPattern","COPY",BODY,{"derivedFrom":makeQuery(id+"F1.opRevolve","SWEPT_BODY",BODY,{"disambiguationData":[OSD([sQuery(id+"F0.wireOp",EDGE,"E1")])]}),"instanceName":"1"}),"instanceName":"1"}),"instanceName":"1"}),"instanceName":"1"}),"instanceName":"1"});
            var Q643;
            Q643=makeQuery(id+"F11.opPattern","COPY",BODY,{"derivedFrom":makeQuery(id+"F10.opPattern","COPY",BODY,{"derivedFrom":makeQuery(id+"F8.opPattern","COPY",BODY,{"derivedFrom":makeQuery(id+"F6.opPattern","COPY",BODY,{"derivedFrom":makeQuery(id+"F5.opPattern","COPY",BODY,{"derivedFrom":makeQuery(id+"F2.opPattern","COPY",BODY,{"derivedFrom":makeQuery(id+"F1.opRevolve","SWEPT_BODY",BODY,{"disambiguationData":[OSD([sQuery(id+"F0.wireOp",EDGE,"E1")])]}),"instanceName":"1"}),"instanceName":"1"}),"instanceName":"1"}),"instanceName":"1"}),"instanceName":"1"}),"instanceName":"1"});
            var Q644;
            Q644=makeQuery(id+"F11.opPattern","COPY",BODY,{"derivedFrom":makeQuery(id+"F10.opPattern","COPY",BODY,{"derivedFrom":makeQuery(id+"F8.opPattern","COPY",BODY,{"derivedFrom":makeQuery(id+"F6.opPattern","COPY",BODY,{"derivedFrom":makeQuery(id+"F5.opPattern","COPY",BODY,{"derivedFrom":makeQuery(id+"F3.opPattern","COPY",BODY,{"derivedFrom":makeQuery(id+"F2.opPattern","COPY",BODY,{"derivedFrom":makeQuery(id+"F1.opRevolve","SWEPT_BODY",BODY,{"disambiguationData":[OSD([sQuery(id+"F0.wireOp",EDGE,"E1")])]}),"instanceName":"1"}),"instanceName":"1"}),"instanceName":"1"}),"instanceName":"1"}),"instanceName":"1"}),"instanceName":"1"}),"instanceName":"1"});
            var Q645;
            Q645=makeQuery(id+"F11.opPattern","COPY",BODY,{"derivedFrom":makeQuery(id+"F10.opPattern","COPY",BODY,{"derivedFrom":makeQuery(id+"F8.opPattern","COPY",BODY,{"derivedFrom":makeQuery(id+"F6.opPattern","COPY",BODY,{"derivedFrom":makeQuery(id+"F5.opPattern","COPY",BODY,{"derivedFrom":makeQuery(id+"F4.opPattern","COPY",BODY,{"derivedFrom":makeQuery(id+"F1.opRevolve","SWEPT_BODY",BODY,{"disambiguationData":[OSD([sQuery(id+"F0.wireOp",EDGE,"E1")])]}),"instanceName":"1"}),"instanceName":"1"}),"instanceName":"1"}),"instanceName":"1"}),"instanceName":"1"}),"instanceName":"1"});
            var Q646;
            Q646=makeQuery(id+"F11.opPattern","COPY",BODY,{"derivedFrom":makeQuery(id+"F10.opPattern","COPY",BODY,{"derivedFrom":makeQuery(id+"F8.opPattern","COPY",BODY,{"derivedFrom":makeQuery(id+"F6.opPattern","COPY",BODY,{"derivedFrom":makeQuery(id+"F5.opPattern","COPY",BODY,{"derivedFrom":makeQuery(id+"F4.opPattern","COPY",BODY,{"derivedFrom":makeQuery(id+"F2.opPattern","COPY",BODY,{"derivedFrom":makeQuery(id+"F1.opRevolve","SWEPT_BODY",BODY,{"disambiguationData":[OSD([sQuery(id+"F0.wireOp",EDGE,"E1")])]}),"instanceName":"1"}),"instanceName":"1"}),"instanceName":"1"}),"instanceName":"1"}),"instanceName":"1"}),"instanceName":"1"}),"instanceName":"1"});
            var Q647;
            Q647=makeQuery(id+"F11.opPattern","COPY",BODY,{"derivedFrom":makeQuery(id+"F10.opPattern","COPY",BODY,{"derivedFrom":makeQuery(id+"F8.opPattern","COPY",BODY,{"derivedFrom":makeQuery(id+"F6.opPattern","COPY",BODY,{"derivedFrom":makeQuery(id+"F5.opPattern","COPY",BODY,{"derivedFrom":makeQuery(id+"F4.opPattern","COPY",BODY,{"derivedFrom":makeQuery(id+"F3.opPattern","COPY",BODY,{"derivedFrom":makeQuery(id+"F2.opPattern","COPY",BODY,{"derivedFrom":makeQuery(id+"F1.opRevolve","SWEPT_BODY",BODY,{"disambiguationData":[OSD([sQuery(id+"F0.wireOp",EDGE,"E1")])]}),"instanceName":"1"}),"instanceName":"1"}),"instanceName":"1"}),"instanceName":"1"}),"instanceName":"1"}),"instanceName":"1"}),"instanceName":"1"}),"instanceName":"1"});
            var Q648;
            Q648=makeQuery(id+"F11.opPattern","COPY",BODY,{"derivedFrom":makeQuery(id+"F10.opPattern","COPY",BODY,{"derivedFrom":makeQuery(id+"F8.opPattern","COPY",BODY,{"derivedFrom":makeQuery(id+"F7.opPattern","COPY",BODY,{"derivedFrom":makeQuery(id+"F1.opRevolve","SWEPT_BODY",BODY,{"disambiguationData":[OSD([sQuery(id+"F0.wireOp",EDGE,"E1")])]}),"instanceName":"1"}),"instanceName":"1"}),"instanceName":"1"}),"instanceName":"1"});
            var Q649;
            Q649=makeQuery(id+"F11.opPattern","COPY",BODY,{"derivedFrom":makeQuery(id+"F10.opPattern","COPY",BODY,{"derivedFrom":makeQuery(id+"F8.opPattern","COPY",BODY,{"derivedFrom":makeQuery(id+"F7.opPattern","COPY",BODY,{"derivedFrom":makeQuery(id+"F2.opPattern","COPY",BODY,{"derivedFrom":makeQuery(id+"F1.opRevolve","SWEPT_BODY",BODY,{"disambiguationData":[OSD([sQuery(id+"F0.wireOp",EDGE,"E1")])]}),"instanceName":"1"}),"instanceName":"1"}),"instanceName":"1"}),"instanceName":"1"}),"instanceName":"1"});
            var Q650;
            Q650=makeQuery(id+"F11.opPattern","COPY",BODY,{"derivedFrom":makeQuery(id+"F10.opPattern","COPY",BODY,{"derivedFrom":makeQuery(id+"F8.opPattern","COPY",BODY,{"derivedFrom":makeQuery(id+"F7.opPattern","COPY",BODY,{"derivedFrom":makeQuery(id+"F3.opPattern","COPY",BODY,{"derivedFrom":makeQuery(id+"F2.opPattern","COPY",BODY,{"derivedFrom":makeQuery(id+"F1.opRevolve","SWEPT_BODY",BODY,{"disambiguationData":[OSD([sQuery(id+"F0.wireOp",EDGE,"E1")])]}),"instanceName":"1"}),"instanceName":"1"}),"instanceName":"1"}),"instanceName":"1"}),"instanceName":"1"}),"instanceName":"1"});
            var Q651;
            Q651=makeQuery(id+"F11.opPattern","COPY",BODY,{"derivedFrom":makeQuery(id+"F10.opPattern","COPY",BODY,{"derivedFrom":makeQuery(id+"F8.opPattern","COPY",BODY,{"derivedFrom":makeQuery(id+"F7.opPattern","COPY",BODY,{"derivedFrom":makeQuery(id+"F4.opPattern","COPY",BODY,{"derivedFrom":makeQuery(id+"F1.opRevolve","SWEPT_BODY",BODY,{"disambiguationData":[OSD([sQuery(id+"F0.wireOp",EDGE,"E1")])]}),"instanceName":"1"}),"instanceName":"1"}),"instanceName":"1"}),"instanceName":"1"}),"instanceName":"1"});
            var Q652;
            Q652=makeQuery(id+"F11.opPattern","COPY",BODY,{"derivedFrom":makeQuery(id+"F10.opPattern","COPY",BODY,{"derivedFrom":makeQuery(id+"F8.opPattern","COPY",BODY,{"derivedFrom":makeQuery(id+"F7.opPattern","COPY",BODY,{"derivedFrom":makeQuery(id+"F4.opPattern","COPY",BODY,{"derivedFrom":makeQuery(id+"F2.opPattern","COPY",BODY,{"derivedFrom":makeQuery(id+"F1.opRevolve","SWEPT_BODY",BODY,{"disambiguationData":[OSD([sQuery(id+"F0.wireOp",EDGE,"E1")])]}),"instanceName":"1"}),"instanceName":"1"}),"instanceName":"1"}),"instanceName":"1"}),"instanceName":"1"}),"instanceName":"1"});
            var Q653;
            Q653=makeQuery(id+"F11.opPattern","COPY",BODY,{"derivedFrom":makeQuery(id+"F10.opPattern","COPY",BODY,{"derivedFrom":makeQuery(id+"F8.opPattern","COPY",BODY,{"derivedFrom":makeQuery(id+"F7.opPattern","COPY",BODY,{"derivedFrom":makeQuery(id+"F4.opPattern","COPY",BODY,{"derivedFrom":makeQuery(id+"F3.opPattern","COPY",BODY,{"derivedFrom":makeQuery(id+"F2.opPattern","COPY",BODY,{"derivedFrom":makeQuery(id+"F1.opRevolve","SWEPT_BODY",BODY,{"disambiguationData":[OSD([sQuery(id+"F0.wireOp",EDGE,"E1")])]}),"instanceName":"1"}),"instanceName":"1"}),"instanceName":"1"}),"instanceName":"1"}),"instanceName":"1"}),"instanceName":"1"}),"instanceName":"1"});
            var Q654;
            Q654=makeQuery(id+"F11.opPattern","COPY",BODY,{"derivedFrom":makeQuery(id+"F10.opPattern","COPY",BODY,{"derivedFrom":makeQuery(id+"F8.opPattern","COPY",BODY,{"derivedFrom":makeQuery(id+"F7.opPattern","COPY",BODY,{"derivedFrom":makeQuery(id+"F5.opPattern","COPY",BODY,{"derivedFrom":makeQuery(id+"F1.opRevolve","SWEPT_BODY",BODY,{"disambiguationData":[OSD([sQuery(id+"F0.wireOp",EDGE,"E1")])]}),"instanceName":"1"}),"instanceName":"1"}),"instanceName":"1"}),"instanceName":"1"}),"instanceName":"1"});
            var Q655;
            Q655=makeQuery(id+"F11.opPattern","COPY",BODY,{"derivedFrom":makeQuery(id+"F10.opPattern","COPY",BODY,{"derivedFrom":makeQuery(id+"F8.opPattern","COPY",BODY,{"derivedFrom":makeQuery(id+"F7.opPattern","COPY",BODY,{"derivedFrom":makeQuery(id+"F5.opPattern","COPY",BODY,{"derivedFrom":makeQuery(id+"F2.opPattern","COPY",BODY,{"derivedFrom":makeQuery(id+"F1.opRevolve","SWEPT_BODY",BODY,{"disambiguationData":[OSD([sQuery(id+"F0.wireOp",EDGE,"E1")])]}),"instanceName":"1"}),"instanceName":"1"}),"instanceName":"1"}),"instanceName":"1"}),"instanceName":"1"}),"instanceName":"1"});
            var Q656;
            Q656=makeQuery(id+"F11.opPattern","COPY",BODY,{"derivedFrom":makeQuery(id+"F10.opPattern","COPY",BODY,{"derivedFrom":makeQuery(id+"F8.opPattern","COPY",BODY,{"derivedFrom":makeQuery(id+"F7.opPattern","COPY",BODY,{"derivedFrom":makeQuery(id+"F5.opPattern","COPY",BODY,{"derivedFrom":makeQuery(id+"F3.opPattern","COPY",BODY,{"derivedFrom":makeQuery(id+"F2.opPattern","COPY",BODY,{"derivedFrom":makeQuery(id+"F1.opRevolve","SWEPT_BODY",BODY,{"disambiguationData":[OSD([sQuery(id+"F0.wireOp",EDGE,"E1")])]}),"instanceName":"1"}),"instanceName":"1"}),"instanceName":"1"}),"instanceName":"1"}),"instanceName":"1"}),"instanceName":"1"}),"instanceName":"1"});
            var Q657;
            Q657=makeQuery(id+"F11.opPattern","COPY",BODY,{"derivedFrom":makeQuery(id+"F10.opPattern","COPY",BODY,{"derivedFrom":makeQuery(id+"F8.opPattern","COPY",BODY,{"derivedFrom":makeQuery(id+"F7.opPattern","COPY",BODY,{"derivedFrom":makeQuery(id+"F5.opPattern","COPY",BODY,{"derivedFrom":makeQuery(id+"F4.opPattern","COPY",BODY,{"derivedFrom":makeQuery(id+"F1.opRevolve","SWEPT_BODY",BODY,{"disambiguationData":[OSD([sQuery(id+"F0.wireOp",EDGE,"E1")])]}),"instanceName":"1"}),"instanceName":"1"}),"instanceName":"1"}),"instanceName":"1"}),"instanceName":"1"}),"instanceName":"1"});
            var Q658;
            Q658=makeQuery(id+"F11.opPattern","COPY",BODY,{"derivedFrom":makeQuery(id+"F10.opPattern","COPY",BODY,{"derivedFrom":makeQuery(id+"F8.opPattern","COPY",BODY,{"derivedFrom":makeQuery(id+"F7.opPattern","COPY",BODY,{"derivedFrom":makeQuery(id+"F5.opPattern","COPY",BODY,{"derivedFrom":makeQuery(id+"F4.opPattern","COPY",BODY,{"derivedFrom":makeQuery(id+"F2.opPattern","COPY",BODY,{"derivedFrom":makeQuery(id+"F1.opRevolve","SWEPT_BODY",BODY,{"disambiguationData":[OSD([sQuery(id+"F0.wireOp",EDGE,"E1")])]}),"instanceName":"1"}),"instanceName":"1"}),"instanceName":"1"}),"instanceName":"1"}),"instanceName":"1"}),"instanceName":"1"}),"instanceName":"1"});
            var Q659;
            Q659=makeQuery(id+"F11.opPattern","COPY",BODY,{"derivedFrom":makeQuery(id+"F10.opPattern","COPY",BODY,{"derivedFrom":makeQuery(id+"F8.opPattern","COPY",BODY,{"derivedFrom":makeQuery(id+"F7.opPattern","COPY",BODY,{"derivedFrom":makeQuery(id+"F5.opPattern","COPY",BODY,{"derivedFrom":makeQuery(id+"F4.opPattern","COPY",BODY,{"derivedFrom":makeQuery(id+"F3.opPattern","COPY",BODY,{"derivedFrom":makeQuery(id+"F2.opPattern","COPY",BODY,{"derivedFrom":makeQuery(id+"F1.opRevolve","SWEPT_BODY",BODY,{"disambiguationData":[OSD([sQuery(id+"F0.wireOp",EDGE,"E1")])]}),"instanceName":"1"}),"instanceName":"1"}),"instanceName":"1"}),"instanceName":"1"}),"instanceName":"1"}),"instanceName":"1"}),"instanceName":"1"}),"instanceName":"1"});
            var Q660;
            Q660=makeQuery(id+"F11.opPattern","COPY",BODY,{"derivedFrom":makeQuery(id+"F10.opPattern","COPY",BODY,{"derivedFrom":makeQuery(id+"F8.opPattern","COPY",BODY,{"derivedFrom":makeQuery(id+"F7.opPattern","COPY",BODY,{"derivedFrom":makeQuery(id+"F6.opPattern","COPY",BODY,{"derivedFrom":makeQuery(id+"F1.opRevolve","SWEPT_BODY",BODY,{"disambiguationData":[OSD([sQuery(id+"F0.wireOp",EDGE,"E1")])]}),"instanceName":"1"}),"instanceName":"1"}),"instanceName":"1"}),"instanceName":"1"}),"instanceName":"1"});
            var Q661;
            Q661=makeQuery(id+"F11.opPattern","COPY",BODY,{"derivedFrom":makeQuery(id+"F10.opPattern","COPY",BODY,{"derivedFrom":makeQuery(id+"F8.opPattern","COPY",BODY,{"derivedFrom":makeQuery(id+"F7.opPattern","COPY",BODY,{"derivedFrom":makeQuery(id+"F6.opPattern","COPY",BODY,{"derivedFrom":makeQuery(id+"F2.opPattern","COPY",BODY,{"derivedFrom":makeQuery(id+"F1.opRevolve","SWEPT_BODY",BODY,{"disambiguationData":[OSD([sQuery(id+"F0.wireOp",EDGE,"E1")])]}),"instanceName":"1"}),"instanceName":"1"}),"instanceName":"1"}),"instanceName":"1"}),"instanceName":"1"}),"instanceName":"1"});
            var Q662;
            Q662=makeQuery(id+"F11.opPattern","COPY",BODY,{"derivedFrom":makeQuery(id+"F10.opPattern","COPY",BODY,{"derivedFrom":makeQuery(id+"F8.opPattern","COPY",BODY,{"derivedFrom":makeQuery(id+"F7.opPattern","COPY",BODY,{"derivedFrom":makeQuery(id+"F6.opPattern","COPY",BODY,{"derivedFrom":makeQuery(id+"F3.opPattern","COPY",BODY,{"derivedFrom":makeQuery(id+"F2.opPattern","COPY",BODY,{"derivedFrom":makeQuery(id+"F1.opRevolve","SWEPT_BODY",BODY,{"disambiguationData":[OSD([sQuery(id+"F0.wireOp",EDGE,"E1")])]}),"instanceName":"1"}),"instanceName":"1"}),"instanceName":"1"}),"instanceName":"1"}),"instanceName":"1"}),"instanceName":"1"}),"instanceName":"1"});
            var Q663;
            Q663=makeQuery(id+"F11.opPattern","COPY",BODY,{"derivedFrom":makeQuery(id+"F10.opPattern","COPY",BODY,{"derivedFrom":makeQuery(id+"F8.opPattern","COPY",BODY,{"derivedFrom":makeQuery(id+"F7.opPattern","COPY",BODY,{"derivedFrom":makeQuery(id+"F6.opPattern","COPY",BODY,{"derivedFrom":makeQuery(id+"F4.opPattern","COPY",BODY,{"derivedFrom":makeQuery(id+"F1.opRevolve","SWEPT_BODY",BODY,{"disambiguationData":[OSD([sQuery(id+"F0.wireOp",EDGE,"E1")])]}),"instanceName":"1"}),"instanceName":"1"}),"instanceName":"1"}),"instanceName":"1"}),"instanceName":"1"}),"instanceName":"1"});
            var Q664;
            Q664=makeQuery(id+"F11.opPattern","COPY",BODY,{"derivedFrom":makeQuery(id+"F10.opPattern","COPY",BODY,{"derivedFrom":makeQuery(id+"F8.opPattern","COPY",BODY,{"derivedFrom":makeQuery(id+"F7.opPattern","COPY",BODY,{"derivedFrom":makeQuery(id+"F6.opPattern","COPY",BODY,{"derivedFrom":makeQuery(id+"F4.opPattern","COPY",BODY,{"derivedFrom":makeQuery(id+"F2.opPattern","COPY",BODY,{"derivedFrom":makeQuery(id+"F1.opRevolve","SWEPT_BODY",BODY,{"disambiguationData":[OSD([sQuery(id+"F0.wireOp",EDGE,"E1")])]}),"instanceName":"1"}),"instanceName":"1"}),"instanceName":"1"}),"instanceName":"1"}),"instanceName":"1"}),"instanceName":"1"}),"instanceName":"1"});
            var Q665;
            Q665=makeQuery(id+"F11.opPattern","COPY",BODY,{"derivedFrom":makeQuery(id+"F10.opPattern","COPY",BODY,{"derivedFrom":makeQuery(id+"F8.opPattern","COPY",BODY,{"derivedFrom":makeQuery(id+"F7.opPattern","COPY",BODY,{"derivedFrom":makeQuery(id+"F6.opPattern","COPY",BODY,{"derivedFrom":makeQuery(id+"F4.opPattern","COPY",BODY,{"derivedFrom":makeQuery(id+"F3.opPattern","COPY",BODY,{"derivedFrom":makeQuery(id+"F2.opPattern","COPY",BODY,{"derivedFrom":makeQuery(id+"F1.opRevolve","SWEPT_BODY",BODY,{"disambiguationData":[OSD([sQuery(id+"F0.wireOp",EDGE,"E1")])]}),"instanceName":"1"}),"instanceName":"1"}),"instanceName":"1"}),"instanceName":"1"}),"instanceName":"1"}),"instanceName":"1"}),"instanceName":"1"}),"instanceName":"1"});
            var Q666;
            Q666=makeQuery(id+"F11.opPattern","COPY",BODY,{"derivedFrom":makeQuery(id+"F10.opPattern","COPY",BODY,{"derivedFrom":makeQuery(id+"F8.opPattern","COPY",BODY,{"derivedFrom":makeQuery(id+"F7.opPattern","COPY",BODY,{"derivedFrom":makeQuery(id+"F6.opPattern","COPY",BODY,{"derivedFrom":makeQuery(id+"F5.opPattern","COPY",BODY,{"derivedFrom":makeQuery(id+"F1.opRevolve","SWEPT_BODY",BODY,{"disambiguationData":[OSD([sQuery(id+"F0.wireOp",EDGE,"E1")])]}),"instanceName":"1"}),"instanceName":"1"}),"instanceName":"1"}),"instanceName":"1"}),"instanceName":"1"}),"instanceName":"1"});
            var Q667;
            Q667=makeQuery(id+"F11.opPattern","COPY",BODY,{"derivedFrom":makeQuery(id+"F10.opPattern","COPY",BODY,{"derivedFrom":makeQuery(id+"F8.opPattern","COPY",BODY,{"derivedFrom":makeQuery(id+"F7.opPattern","COPY",BODY,{"derivedFrom":makeQuery(id+"F6.opPattern","COPY",BODY,{"derivedFrom":makeQuery(id+"F5.opPattern","COPY",BODY,{"derivedFrom":makeQuery(id+"F2.opPattern","COPY",BODY,{"derivedFrom":makeQuery(id+"F1.opRevolve","SWEPT_BODY",BODY,{"disambiguationData":[OSD([sQuery(id+"F0.wireOp",EDGE,"E1")])]}),"instanceName":"1"}),"instanceName":"1"}),"instanceName":"1"}),"instanceName":"1"}),"instanceName":"1"}),"instanceName":"1"}),"instanceName":"1"});
            var Q668;
            Q668=makeQuery(id+"F11.opPattern","COPY",BODY,{"derivedFrom":makeQuery(id+"F10.opPattern","COPY",BODY,{"derivedFrom":makeQuery(id+"F8.opPattern","COPY",BODY,{"derivedFrom":makeQuery(id+"F7.opPattern","COPY",BODY,{"derivedFrom":makeQuery(id+"F6.opPattern","COPY",BODY,{"derivedFrom":makeQuery(id+"F5.opPattern","COPY",BODY,{"derivedFrom":makeQuery(id+"F3.opPattern","COPY",BODY,{"derivedFrom":makeQuery(id+"F2.opPattern","COPY",BODY,{"derivedFrom":makeQuery(id+"F1.opRevolve","SWEPT_BODY",BODY,{"disambiguationData":[OSD([sQuery(id+"F0.wireOp",EDGE,"E1")])]}),"instanceName":"1"}),"instanceName":"1"}),"instanceName":"1"}),"instanceName":"1"}),"instanceName":"1"}),"instanceName":"1"}),"instanceName":"1"}),"instanceName":"1"});
            var Q669;
            Q669=makeQuery(id+"F11.opPattern","COPY",BODY,{"derivedFrom":makeQuery(id+"F10.opPattern","COPY",BODY,{"derivedFrom":makeQuery(id+"F8.opPattern","COPY",BODY,{"derivedFrom":makeQuery(id+"F7.opPattern","COPY",BODY,{"derivedFrom":makeQuery(id+"F6.opPattern","COPY",BODY,{"derivedFrom":makeQuery(id+"F5.opPattern","COPY",BODY,{"derivedFrom":makeQuery(id+"F4.opPattern","COPY",BODY,{"derivedFrom":makeQuery(id+"F1.opRevolve","SWEPT_BODY",BODY,{"disambiguationData":[OSD([sQuery(id+"F0.wireOp",EDGE,"E1")])]}),"instanceName":"1"}),"instanceName":"1"}),"instanceName":"1"}),"instanceName":"1"}),"instanceName":"1"}),"instanceName":"1"}),"instanceName":"1"});
            var Q670;
            Q670=makeQuery(id+"F11.opPattern","COPY",BODY,{"derivedFrom":makeQuery(id+"F10.opPattern","COPY",BODY,{"derivedFrom":makeQuery(id+"F8.opPattern","COPY",BODY,{"derivedFrom":makeQuery(id+"F7.opPattern","COPY",BODY,{"derivedFrom":makeQuery(id+"F6.opPattern","COPY",BODY,{"derivedFrom":makeQuery(id+"F5.opPattern","COPY",BODY,{"derivedFrom":makeQuery(id+"F4.opPattern","COPY",BODY,{"derivedFrom":makeQuery(id+"F2.opPattern","COPY",BODY,{"derivedFrom":makeQuery(id+"F1.opRevolve","SWEPT_BODY",BODY,{"disambiguationData":[OSD([sQuery(id+"F0.wireOp",EDGE,"E1")])]}),"instanceName":"1"}),"instanceName":"1"}),"instanceName":"1"}),"instanceName":"1"}),"instanceName":"1"}),"instanceName":"1"}),"instanceName":"1"}),"instanceName":"1"});
            var Q671;
            Q671=makeQuery(id+"F11.opPattern","COPY",BODY,{"derivedFrom":makeQuery(id+"F10.opPattern","COPY",BODY,{"derivedFrom":makeQuery(id+"F8.opPattern","COPY",BODY,{"derivedFrom":makeQuery(id+"F7.opPattern","COPY",BODY,{"derivedFrom":makeQuery(id+"F6.opPattern","COPY",BODY,{"derivedFrom":makeQuery(id+"F5.opPattern","COPY",BODY,{"derivedFrom":makeQuery(id+"F4.opPattern","COPY",BODY,{"derivedFrom":makeQuery(id+"F3.opPattern","COPY",BODY,{"derivedFrom":makeQuery(id+"F2.opPattern","COPY",BODY,{"derivedFrom":makeQuery(id+"F1.opRevolve","SWEPT_BODY",BODY,{"disambiguationData":[OSD([sQuery(id+"F0.wireOp",EDGE,"E1")])]}),"instanceName":"1"}),"instanceName":"1"}),"instanceName":"1"}),"instanceName":"1"}),"instanceName":"1"}),"instanceName":"1"}),"instanceName":"1"}),"instanceName":"1"}),"instanceName":"1"});
            var Q672;
            Q672=makeQuery(id+"F11.opPattern","COPY",BODY,{"derivedFrom":makeQuery(id+"F10.opPattern","COPY",BODY,{"derivedFrom":makeQuery(id+"F9.opPattern","COPY",BODY,{"derivedFrom":makeQuery(id+"F1.opRevolve","SWEPT_BODY",BODY,{"disambiguationData":[OSD([sQuery(id+"F0.wireOp",EDGE,"E1")])]}),"instanceName":"1"}),"instanceName":"1"}),"instanceName":"1"});
            var Q673;
            Q673=makeQuery(id+"F11.opPattern","COPY",BODY,{"derivedFrom":makeQuery(id+"F10.opPattern","COPY",BODY,{"derivedFrom":makeQuery(id+"F9.opPattern","COPY",BODY,{"derivedFrom":makeQuery(id+"F2.opPattern","COPY",BODY,{"derivedFrom":makeQuery(id+"F1.opRevolve","SWEPT_BODY",BODY,{"disambiguationData":[OSD([sQuery(id+"F0.wireOp",EDGE,"E1")])]}),"instanceName":"1"}),"instanceName":"1"}),"instanceName":"1"}),"instanceName":"1"});
            var Q674;
            Q674=makeQuery(id+"F11.opPattern","COPY",BODY,{"derivedFrom":makeQuery(id+"F10.opPattern","COPY",BODY,{"derivedFrom":makeQuery(id+"F9.opPattern","COPY",BODY,{"derivedFrom":makeQuery(id+"F3.opPattern","COPY",BODY,{"derivedFrom":makeQuery(id+"F2.opPattern","COPY",BODY,{"derivedFrom":makeQuery(id+"F1.opRevolve","SWEPT_BODY",BODY,{"disambiguationData":[OSD([sQuery(id+"F0.wireOp",EDGE,"E1")])]}),"instanceName":"1"}),"instanceName":"1"}),"instanceName":"1"}),"instanceName":"1"}),"instanceName":"1"});
            var Q675;
            Q675=makeQuery(id+"F11.opPattern","COPY",BODY,{"derivedFrom":makeQuery(id+"F10.opPattern","COPY",BODY,{"derivedFrom":makeQuery(id+"F9.opPattern","COPY",BODY,{"derivedFrom":makeQuery(id+"F4.opPattern","COPY",BODY,{"derivedFrom":makeQuery(id+"F1.opRevolve","SWEPT_BODY",BODY,{"disambiguationData":[OSD([sQuery(id+"F0.wireOp",EDGE,"E1")])]}),"instanceName":"1"}),"instanceName":"1"}),"instanceName":"1"}),"instanceName":"1"});
            var Q676;
            Q676=makeQuery(id+"F11.opPattern","COPY",BODY,{"derivedFrom":makeQuery(id+"F10.opPattern","COPY",BODY,{"derivedFrom":makeQuery(id+"F9.opPattern","COPY",BODY,{"derivedFrom":makeQuery(id+"F4.opPattern","COPY",BODY,{"derivedFrom":makeQuery(id+"F2.opPattern","COPY",BODY,{"derivedFrom":makeQuery(id+"F1.opRevolve","SWEPT_BODY",BODY,{"disambiguationData":[OSD([sQuery(id+"F0.wireOp",EDGE,"E1")])]}),"instanceName":"1"}),"instanceName":"1"}),"instanceName":"1"}),"instanceName":"1"}),"instanceName":"1"});
            var Q677;
            Q677=makeQuery(id+"F11.opPattern","COPY",BODY,{"derivedFrom":makeQuery(id+"F10.opPattern","COPY",BODY,{"derivedFrom":makeQuery(id+"F9.opPattern","COPY",BODY,{"derivedFrom":makeQuery(id+"F4.opPattern","COPY",BODY,{"derivedFrom":makeQuery(id+"F3.opPattern","COPY",BODY,{"derivedFrom":makeQuery(id+"F2.opPattern","COPY",BODY,{"derivedFrom":makeQuery(id+"F1.opRevolve","SWEPT_BODY",BODY,{"disambiguationData":[OSD([sQuery(id+"F0.wireOp",EDGE,"E1")])]}),"instanceName":"1"}),"instanceName":"1"}),"instanceName":"1"}),"instanceName":"1"}),"instanceName":"1"}),"instanceName":"1"});
            var Q678;
            Q678=makeQuery(id+"F11.opPattern","COPY",BODY,{"derivedFrom":makeQuery(id+"F10.opPattern","COPY",BODY,{"derivedFrom":makeQuery(id+"F9.opPattern","COPY",BODY,{"derivedFrom":makeQuery(id+"F5.opPattern","COPY",BODY,{"derivedFrom":makeQuery(id+"F1.opRevolve","SWEPT_BODY",BODY,{"disambiguationData":[OSD([sQuery(id+"F0.wireOp",EDGE,"E1")])]}),"instanceName":"1"}),"instanceName":"1"}),"instanceName":"1"}),"instanceName":"1"});
            var Q679;
            Q679=makeQuery(id+"F11.opPattern","COPY",BODY,{"derivedFrom":makeQuery(id+"F10.opPattern","COPY",BODY,{"derivedFrom":makeQuery(id+"F9.opPattern","COPY",BODY,{"derivedFrom":makeQuery(id+"F5.opPattern","COPY",BODY,{"derivedFrom":makeQuery(id+"F2.opPattern","COPY",BODY,{"derivedFrom":makeQuery(id+"F1.opRevolve","SWEPT_BODY",BODY,{"disambiguationData":[OSD([sQuery(id+"F0.wireOp",EDGE,"E1")])]}),"instanceName":"1"}),"instanceName":"1"}),"instanceName":"1"}),"instanceName":"1"}),"instanceName":"1"});
            var Q680;
            Q680=makeQuery(id+"F11.opPattern","COPY",BODY,{"derivedFrom":makeQuery(id+"F10.opPattern","COPY",BODY,{"derivedFrom":makeQuery(id+"F9.opPattern","COPY",BODY,{"derivedFrom":makeQuery(id+"F5.opPattern","COPY",BODY,{"derivedFrom":makeQuery(id+"F3.opPattern","COPY",BODY,{"derivedFrom":makeQuery(id+"F2.opPattern","COPY",BODY,{"derivedFrom":makeQuery(id+"F1.opRevolve","SWEPT_BODY",BODY,{"disambiguationData":[OSD([sQuery(id+"F0.wireOp",EDGE,"E1")])]}),"instanceName":"1"}),"instanceName":"1"}),"instanceName":"1"}),"instanceName":"1"}),"instanceName":"1"}),"instanceName":"1"});
            var Q681;
            Q681=makeQuery(id+"F11.opPattern","COPY",BODY,{"derivedFrom":makeQuery(id+"F10.opPattern","COPY",BODY,{"derivedFrom":makeQuery(id+"F9.opPattern","COPY",BODY,{"derivedFrom":makeQuery(id+"F5.opPattern","COPY",BODY,{"derivedFrom":makeQuery(id+"F4.opPattern","COPY",BODY,{"derivedFrom":makeQuery(id+"F1.opRevolve","SWEPT_BODY",BODY,{"disambiguationData":[OSD([sQuery(id+"F0.wireOp",EDGE,"E1")])]}),"instanceName":"1"}),"instanceName":"1"}),"instanceName":"1"}),"instanceName":"1"}),"instanceName":"1"});
            var Q682;
            Q682=makeQuery(id+"F11.opPattern","COPY",BODY,{"derivedFrom":makeQuery(id+"F10.opPattern","COPY",BODY,{"derivedFrom":makeQuery(id+"F9.opPattern","COPY",BODY,{"derivedFrom":makeQuery(id+"F5.opPattern","COPY",BODY,{"derivedFrom":makeQuery(id+"F4.opPattern","COPY",BODY,{"derivedFrom":makeQuery(id+"F2.opPattern","COPY",BODY,{"derivedFrom":makeQuery(id+"F1.opRevolve","SWEPT_BODY",BODY,{"disambiguationData":[OSD([sQuery(id+"F0.wireOp",EDGE,"E1")])]}),"instanceName":"1"}),"instanceName":"1"}),"instanceName":"1"}),"instanceName":"1"}),"instanceName":"1"}),"instanceName":"1"});
            var Q683;
            Q683=makeQuery(id+"F11.opPattern","COPY",BODY,{"derivedFrom":makeQuery(id+"F10.opPattern","COPY",BODY,{"derivedFrom":makeQuery(id+"F9.opPattern","COPY",BODY,{"derivedFrom":makeQuery(id+"F5.opPattern","COPY",BODY,{"derivedFrom":makeQuery(id+"F4.opPattern","COPY",BODY,{"derivedFrom":makeQuery(id+"F3.opPattern","COPY",BODY,{"derivedFrom":makeQuery(id+"F2.opPattern","COPY",BODY,{"derivedFrom":makeQuery(id+"F1.opRevolve","SWEPT_BODY",BODY,{"disambiguationData":[OSD([sQuery(id+"F0.wireOp",EDGE,"E1")])]}),"instanceName":"1"}),"instanceName":"1"}),"instanceName":"1"}),"instanceName":"1"}),"instanceName":"1"}),"instanceName":"1"}),"instanceName":"1"});
            var Q684;
            Q684=makeQuery(id+"F11.opPattern","COPY",BODY,{"derivedFrom":makeQuery(id+"F10.opPattern","COPY",BODY,{"derivedFrom":makeQuery(id+"F9.opPattern","COPY",BODY,{"derivedFrom":makeQuery(id+"F6.opPattern","COPY",BODY,{"derivedFrom":makeQuery(id+"F1.opRevolve","SWEPT_BODY",BODY,{"disambiguationData":[OSD([sQuery(id+"F0.wireOp",EDGE,"E1")])]}),"instanceName":"1"}),"instanceName":"1"}),"instanceName":"1"}),"instanceName":"1"});
            var Q685;
            Q685=makeQuery(id+"F11.opPattern","COPY",BODY,{"derivedFrom":makeQuery(id+"F10.opPattern","COPY",BODY,{"derivedFrom":makeQuery(id+"F9.opPattern","COPY",BODY,{"derivedFrom":makeQuery(id+"F6.opPattern","COPY",BODY,{"derivedFrom":makeQuery(id+"F2.opPattern","COPY",BODY,{"derivedFrom":makeQuery(id+"F1.opRevolve","SWEPT_BODY",BODY,{"disambiguationData":[OSD([sQuery(id+"F0.wireOp",EDGE,"E1")])]}),"instanceName":"1"}),"instanceName":"1"}),"instanceName":"1"}),"instanceName":"1"}),"instanceName":"1"});
            var Q686;
            Q686=makeQuery(id+"F11.opPattern","COPY",BODY,{"derivedFrom":makeQuery(id+"F10.opPattern","COPY",BODY,{"derivedFrom":makeQuery(id+"F9.opPattern","COPY",BODY,{"derivedFrom":makeQuery(id+"F6.opPattern","COPY",BODY,{"derivedFrom":makeQuery(id+"F3.opPattern","COPY",BODY,{"derivedFrom":makeQuery(id+"F2.opPattern","COPY",BODY,{"derivedFrom":makeQuery(id+"F1.opRevolve","SWEPT_BODY",BODY,{"disambiguationData":[OSD([sQuery(id+"F0.wireOp",EDGE,"E1")])]}),"instanceName":"1"}),"instanceName":"1"}),"instanceName":"1"}),"instanceName":"1"}),"instanceName":"1"}),"instanceName":"1"});
            var Q687;
            Q687=makeQuery(id+"F11.opPattern","COPY",BODY,{"derivedFrom":makeQuery(id+"F10.opPattern","COPY",BODY,{"derivedFrom":makeQuery(id+"F9.opPattern","COPY",BODY,{"derivedFrom":makeQuery(id+"F6.opPattern","COPY",BODY,{"derivedFrom":makeQuery(id+"F4.opPattern","COPY",BODY,{"derivedFrom":makeQuery(id+"F1.opRevolve","SWEPT_BODY",BODY,{"disambiguationData":[OSD([sQuery(id+"F0.wireOp",EDGE,"E1")])]}),"instanceName":"1"}),"instanceName":"1"}),"instanceName":"1"}),"instanceName":"1"}),"instanceName":"1"});
            var Q688;
            Q688=makeQuery(id+"F11.opPattern","COPY",BODY,{"derivedFrom":makeQuery(id+"F10.opPattern","COPY",BODY,{"derivedFrom":makeQuery(id+"F9.opPattern","COPY",BODY,{"derivedFrom":makeQuery(id+"F6.opPattern","COPY",BODY,{"derivedFrom":makeQuery(id+"F4.opPattern","COPY",BODY,{"derivedFrom":makeQuery(id+"F2.opPattern","COPY",BODY,{"derivedFrom":makeQuery(id+"F1.opRevolve","SWEPT_BODY",BODY,{"disambiguationData":[OSD([sQuery(id+"F0.wireOp",EDGE,"E1")])]}),"instanceName":"1"}),"instanceName":"1"}),"instanceName":"1"}),"instanceName":"1"}),"instanceName":"1"}),"instanceName":"1"});
            var Q689;
            Q689=makeQuery(id+"F11.opPattern","COPY",BODY,{"derivedFrom":makeQuery(id+"F10.opPattern","COPY",BODY,{"derivedFrom":makeQuery(id+"F9.opPattern","COPY",BODY,{"derivedFrom":makeQuery(id+"F6.opPattern","COPY",BODY,{"derivedFrom":makeQuery(id+"F4.opPattern","COPY",BODY,{"derivedFrom":makeQuery(id+"F3.opPattern","COPY",BODY,{"derivedFrom":makeQuery(id+"F2.opPattern","COPY",BODY,{"derivedFrom":makeQuery(id+"F1.opRevolve","SWEPT_BODY",BODY,{"disambiguationData":[OSD([sQuery(id+"F0.wireOp",EDGE,"E1")])]}),"instanceName":"1"}),"instanceName":"1"}),"instanceName":"1"}),"instanceName":"1"}),"instanceName":"1"}),"instanceName":"1"}),"instanceName":"1"});
            var Q690;
            Q690=makeQuery(id+"F11.opPattern","COPY",BODY,{"derivedFrom":makeQuery(id+"F10.opPattern","COPY",BODY,{"derivedFrom":makeQuery(id+"F9.opPattern","COPY",BODY,{"derivedFrom":makeQuery(id+"F6.opPattern","COPY",BODY,{"derivedFrom":makeQuery(id+"F5.opPattern","COPY",BODY,{"derivedFrom":makeQuery(id+"F1.opRevolve","SWEPT_BODY",BODY,{"disambiguationData":[OSD([sQuery(id+"F0.wireOp",EDGE,"E1")])]}),"instanceName":"1"}),"instanceName":"1"}),"instanceName":"1"}),"instanceName":"1"}),"instanceName":"1"});
            var Q691;
            Q691=makeQuery(id+"F11.opPattern","COPY",BODY,{"derivedFrom":makeQuery(id+"F10.opPattern","COPY",BODY,{"derivedFrom":makeQuery(id+"F9.opPattern","COPY",BODY,{"derivedFrom":makeQuery(id+"F6.opPattern","COPY",BODY,{"derivedFrom":makeQuery(id+"F5.opPattern","COPY",BODY,{"derivedFrom":makeQuery(id+"F2.opPattern","COPY",BODY,{"derivedFrom":makeQuery(id+"F1.opRevolve","SWEPT_BODY",BODY,{"disambiguationData":[OSD([sQuery(id+"F0.wireOp",EDGE,"E1")])]}),"instanceName":"1"}),"instanceName":"1"}),"instanceName":"1"}),"instanceName":"1"}),"instanceName":"1"}),"instanceName":"1"});
            var Q692;
            Q692=makeQuery(id+"F11.opPattern","COPY",BODY,{"derivedFrom":makeQuery(id+"F10.opPattern","COPY",BODY,{"derivedFrom":makeQuery(id+"F9.opPattern","COPY",BODY,{"derivedFrom":makeQuery(id+"F6.opPattern","COPY",BODY,{"derivedFrom":makeQuery(id+"F5.opPattern","COPY",BODY,{"derivedFrom":makeQuery(id+"F3.opPattern","COPY",BODY,{"derivedFrom":makeQuery(id+"F2.opPattern","COPY",BODY,{"derivedFrom":makeQuery(id+"F1.opRevolve","SWEPT_BODY",BODY,{"disambiguationData":[OSD([sQuery(id+"F0.wireOp",EDGE,"E1")])]}),"instanceName":"1"}),"instanceName":"1"}),"instanceName":"1"}),"instanceName":"1"}),"instanceName":"1"}),"instanceName":"1"}),"instanceName":"1"});
            var Q693;
            Q693=makeQuery(id+"F11.opPattern","COPY",BODY,{"derivedFrom":makeQuery(id+"F10.opPattern","COPY",BODY,{"derivedFrom":makeQuery(id+"F9.opPattern","COPY",BODY,{"derivedFrom":makeQuery(id+"F6.opPattern","COPY",BODY,{"derivedFrom":makeQuery(id+"F5.opPattern","COPY",BODY,{"derivedFrom":makeQuery(id+"F4.opPattern","COPY",BODY,{"derivedFrom":makeQuery(id+"F1.opRevolve","SWEPT_BODY",BODY,{"disambiguationData":[OSD([sQuery(id+"F0.wireOp",EDGE,"E1")])]}),"instanceName":"1"}),"instanceName":"1"}),"instanceName":"1"}),"instanceName":"1"}),"instanceName":"1"}),"instanceName":"1"});
            var Q694;
            Q694=makeQuery(id+"F11.opPattern","COPY",BODY,{"derivedFrom":makeQuery(id+"F10.opPattern","COPY",BODY,{"derivedFrom":makeQuery(id+"F9.opPattern","COPY",BODY,{"derivedFrom":makeQuery(id+"F6.opPattern","COPY",BODY,{"derivedFrom":makeQuery(id+"F5.opPattern","COPY",BODY,{"derivedFrom":makeQuery(id+"F4.opPattern","COPY",BODY,{"derivedFrom":makeQuery(id+"F2.opPattern","COPY",BODY,{"derivedFrom":makeQuery(id+"F1.opRevolve","SWEPT_BODY",BODY,{"disambiguationData":[OSD([sQuery(id+"F0.wireOp",EDGE,"E1")])]}),"instanceName":"1"}),"instanceName":"1"}),"instanceName":"1"}),"instanceName":"1"}),"instanceName":"1"}),"instanceName":"1"}),"instanceName":"1"});
            var Q695;
            Q695=makeQuery(id+"F11.opPattern","COPY",BODY,{"derivedFrom":makeQuery(id+"F10.opPattern","COPY",BODY,{"derivedFrom":makeQuery(id+"F9.opPattern","COPY",BODY,{"derivedFrom":makeQuery(id+"F6.opPattern","COPY",BODY,{"derivedFrom":makeQuery(id+"F5.opPattern","COPY",BODY,{"derivedFrom":makeQuery(id+"F4.opPattern","COPY",BODY,{"derivedFrom":makeQuery(id+"F3.opPattern","COPY",BODY,{"derivedFrom":makeQuery(id+"F2.opPattern","COPY",BODY,{"derivedFrom":makeQuery(id+"F1.opRevolve","SWEPT_BODY",BODY,{"disambiguationData":[OSD([sQuery(id+"F0.wireOp",EDGE,"E1")])]}),"instanceName":"1"}),"instanceName":"1"}),"instanceName":"1"}),"instanceName":"1"}),"instanceName":"1"}),"instanceName":"1"}),"instanceName":"1"}),"instanceName":"1"});
            var Q696;
            Q696=makeQuery(id+"F11.opPattern","COPY",BODY,{"derivedFrom":makeQuery(id+"F10.opPattern","COPY",BODY,{"derivedFrom":makeQuery(id+"F9.opPattern","COPY",BODY,{"derivedFrom":makeQuery(id+"F7.opPattern","COPY",BODY,{"derivedFrom":makeQuery(id+"F1.opRevolve","SWEPT_BODY",BODY,{"disambiguationData":[OSD([sQuery(id+"F0.wireOp",EDGE,"E1")])]}),"instanceName":"1"}),"instanceName":"1"}),"instanceName":"1"}),"instanceName":"1"});
            var Q697;
            Q697=makeQuery(id+"F11.opPattern","COPY",BODY,{"derivedFrom":makeQuery(id+"F10.opPattern","COPY",BODY,{"derivedFrom":makeQuery(id+"F9.opPattern","COPY",BODY,{"derivedFrom":makeQuery(id+"F7.opPattern","COPY",BODY,{"derivedFrom":makeQuery(id+"F2.opPattern","COPY",BODY,{"derivedFrom":makeQuery(id+"F1.opRevolve","SWEPT_BODY",BODY,{"disambiguationData":[OSD([sQuery(id+"F0.wireOp",EDGE,"E1")])]}),"instanceName":"1"}),"instanceName":"1"}),"instanceName":"1"}),"instanceName":"1"}),"instanceName":"1"});
            var Q698;
            Q698=makeQuery(id+"F11.opPattern","COPY",BODY,{"derivedFrom":makeQuery(id+"F10.opPattern","COPY",BODY,{"derivedFrom":makeQuery(id+"F9.opPattern","COPY",BODY,{"derivedFrom":makeQuery(id+"F7.opPattern","COPY",BODY,{"derivedFrom":makeQuery(id+"F3.opPattern","COPY",BODY,{"derivedFrom":makeQuery(id+"F2.opPattern","COPY",BODY,{"derivedFrom":makeQuery(id+"F1.opRevolve","SWEPT_BODY",BODY,{"disambiguationData":[OSD([sQuery(id+"F0.wireOp",EDGE,"E1")])]}),"instanceName":"1"}),"instanceName":"1"}),"instanceName":"1"}),"instanceName":"1"}),"instanceName":"1"}),"instanceName":"1"});
            var Q699;
            Q699=makeQuery(id+"F11.opPattern","COPY",BODY,{"derivedFrom":makeQuery(id+"F10.opPattern","COPY",BODY,{"derivedFrom":makeQuery(id+"F9.opPattern","COPY",BODY,{"derivedFrom":makeQuery(id+"F7.opPattern","COPY",BODY,{"derivedFrom":makeQuery(id+"F4.opPattern","COPY",BODY,{"derivedFrom":makeQuery(id+"F1.opRevolve","SWEPT_BODY",BODY,{"disambiguationData":[OSD([sQuery(id+"F0.wireOp",EDGE,"E1")])]}),"instanceName":"1"}),"instanceName":"1"}),"instanceName":"1"}),"instanceName":"1"}),"instanceName":"1"});
            var Q700;
            Q700=makeQuery(id+"F11.opPattern","COPY",BODY,{"derivedFrom":makeQuery(id+"F10.opPattern","COPY",BODY,{"derivedFrom":makeQuery(id+"F9.opPattern","COPY",BODY,{"derivedFrom":makeQuery(id+"F7.opPattern","COPY",BODY,{"derivedFrom":makeQuery(id+"F4.opPattern","COPY",BODY,{"derivedFrom":makeQuery(id+"F2.opPattern","COPY",BODY,{"derivedFrom":makeQuery(id+"F1.opRevolve","SWEPT_BODY",BODY,{"disambiguationData":[OSD([sQuery(id+"F0.wireOp",EDGE,"E1")])]}),"instanceName":"1"}),"instanceName":"1"}),"instanceName":"1"}),"instanceName":"1"}),"instanceName":"1"}),"instanceName":"1"});
            var Q701;
            Q701=makeQuery(id+"F11.opPattern","COPY",BODY,{"derivedFrom":makeQuery(id+"F10.opPattern","COPY",BODY,{"derivedFrom":makeQuery(id+"F9.opPattern","COPY",BODY,{"derivedFrom":makeQuery(id+"F7.opPattern","COPY",BODY,{"derivedFrom":makeQuery(id+"F4.opPattern","COPY",BODY,{"derivedFrom":makeQuery(id+"F3.opPattern","COPY",BODY,{"derivedFrom":makeQuery(id+"F2.opPattern","COPY",BODY,{"derivedFrom":makeQuery(id+"F1.opRevolve","SWEPT_BODY",BODY,{"disambiguationData":[OSD([sQuery(id+"F0.wireOp",EDGE,"E1")])]}),"instanceName":"1"}),"instanceName":"1"}),"instanceName":"1"}),"instanceName":"1"}),"instanceName":"1"}),"instanceName":"1"}),"instanceName":"1"});
            var Q702;
            Q702=makeQuery(id+"F11.opPattern","COPY",BODY,{"derivedFrom":makeQuery(id+"F10.opPattern","COPY",BODY,{"derivedFrom":makeQuery(id+"F9.opPattern","COPY",BODY,{"derivedFrom":makeQuery(id+"F7.opPattern","COPY",BODY,{"derivedFrom":makeQuery(id+"F5.opPattern","COPY",BODY,{"derivedFrom":makeQuery(id+"F1.opRevolve","SWEPT_BODY",BODY,{"disambiguationData":[OSD([sQuery(id+"F0.wireOp",EDGE,"E1")])]}),"instanceName":"1"}),"instanceName":"1"}),"instanceName":"1"}),"instanceName":"1"}),"instanceName":"1"});
            var Q703;
            Q703=makeQuery(id+"F11.opPattern","COPY",BODY,{"derivedFrom":makeQuery(id+"F10.opPattern","COPY",BODY,{"derivedFrom":makeQuery(id+"F9.opPattern","COPY",BODY,{"derivedFrom":makeQuery(id+"F7.opPattern","COPY",BODY,{"derivedFrom":makeQuery(id+"F5.opPattern","COPY",BODY,{"derivedFrom":makeQuery(id+"F2.opPattern","COPY",BODY,{"derivedFrom":makeQuery(id+"F1.opRevolve","SWEPT_BODY",BODY,{"disambiguationData":[OSD([sQuery(id+"F0.wireOp",EDGE,"E1")])]}),"instanceName":"1"}),"instanceName":"1"}),"instanceName":"1"}),"instanceName":"1"}),"instanceName":"1"}),"instanceName":"1"});
            var Q704;
            Q704=makeQuery(id+"F11.opPattern","COPY",BODY,{"derivedFrom":makeQuery(id+"F10.opPattern","COPY",BODY,{"derivedFrom":makeQuery(id+"F9.opPattern","COPY",BODY,{"derivedFrom":makeQuery(id+"F7.opPattern","COPY",BODY,{"derivedFrom":makeQuery(id+"F5.opPattern","COPY",BODY,{"derivedFrom":makeQuery(id+"F3.opPattern","COPY",BODY,{"derivedFrom":makeQuery(id+"F2.opPattern","COPY",BODY,{"derivedFrom":makeQuery(id+"F1.opRevolve","SWEPT_BODY",BODY,{"disambiguationData":[OSD([sQuery(id+"F0.wireOp",EDGE,"E1")])]}),"instanceName":"1"}),"instanceName":"1"}),"instanceName":"1"}),"instanceName":"1"}),"instanceName":"1"}),"instanceName":"1"}),"instanceName":"1"});
            var Q705;
            Q705=makeQuery(id+"F11.opPattern","COPY",BODY,{"derivedFrom":makeQuery(id+"F10.opPattern","COPY",BODY,{"derivedFrom":makeQuery(id+"F9.opPattern","COPY",BODY,{"derivedFrom":makeQuery(id+"F7.opPattern","COPY",BODY,{"derivedFrom":makeQuery(id+"F5.opPattern","COPY",BODY,{"derivedFrom":makeQuery(id+"F4.opPattern","COPY",BODY,{"derivedFrom":makeQuery(id+"F1.opRevolve","SWEPT_BODY",BODY,{"disambiguationData":[OSD([sQuery(id+"F0.wireOp",EDGE,"E1")])]}),"instanceName":"1"}),"instanceName":"1"}),"instanceName":"1"}),"instanceName":"1"}),"instanceName":"1"}),"instanceName":"1"});
            var Q706;
            Q706=makeQuery(id+"F11.opPattern","COPY",BODY,{"derivedFrom":makeQuery(id+"F10.opPattern","COPY",BODY,{"derivedFrom":makeQuery(id+"F9.opPattern","COPY",BODY,{"derivedFrom":makeQuery(id+"F7.opPattern","COPY",BODY,{"derivedFrom":makeQuery(id+"F5.opPattern","COPY",BODY,{"derivedFrom":makeQuery(id+"F4.opPattern","COPY",BODY,{"derivedFrom":makeQuery(id+"F2.opPattern","COPY",BODY,{"derivedFrom":makeQuery(id+"F1.opRevolve","SWEPT_BODY",BODY,{"disambiguationData":[OSD([sQuery(id+"F0.wireOp",EDGE,"E1")])]}),"instanceName":"1"}),"instanceName":"1"}),"instanceName":"1"}),"instanceName":"1"}),"instanceName":"1"}),"instanceName":"1"}),"instanceName":"1"});
            var Q707;
            Q707=makeQuery(id+"F11.opPattern","COPY",BODY,{"derivedFrom":makeQuery(id+"F10.opPattern","COPY",BODY,{"derivedFrom":makeQuery(id+"F9.opPattern","COPY",BODY,{"derivedFrom":makeQuery(id+"F7.opPattern","COPY",BODY,{"derivedFrom":makeQuery(id+"F5.opPattern","COPY",BODY,{"derivedFrom":makeQuery(id+"F4.opPattern","COPY",BODY,{"derivedFrom":makeQuery(id+"F3.opPattern","COPY",BODY,{"derivedFrom":makeQuery(id+"F2.opPattern","COPY",BODY,{"derivedFrom":makeQuery(id+"F1.opRevolve","SWEPT_BODY",BODY,{"disambiguationData":[OSD([sQuery(id+"F0.wireOp",EDGE,"E1")])]}),"instanceName":"1"}),"instanceName":"1"}),"instanceName":"1"}),"instanceName":"1"}),"instanceName":"1"}),"instanceName":"1"}),"instanceName":"1"}),"instanceName":"1"});
            var Q708;
            Q708=makeQuery(id+"F11.opPattern","COPY",BODY,{"derivedFrom":makeQuery(id+"F10.opPattern","COPY",BODY,{"derivedFrom":makeQuery(id+"F9.opPattern","COPY",BODY,{"derivedFrom":makeQuery(id+"F7.opPattern","COPY",BODY,{"derivedFrom":makeQuery(id+"F6.opPattern","COPY",BODY,{"derivedFrom":makeQuery(id+"F1.opRevolve","SWEPT_BODY",BODY,{"disambiguationData":[OSD([sQuery(id+"F0.wireOp",EDGE,"E1")])]}),"instanceName":"1"}),"instanceName":"1"}),"instanceName":"1"}),"instanceName":"1"}),"instanceName":"1"});
            var Q709;
            Q709=makeQuery(id+"F11.opPattern","COPY",BODY,{"derivedFrom":makeQuery(id+"F10.opPattern","COPY",BODY,{"derivedFrom":makeQuery(id+"F9.opPattern","COPY",BODY,{"derivedFrom":makeQuery(id+"F7.opPattern","COPY",BODY,{"derivedFrom":makeQuery(id+"F6.opPattern","COPY",BODY,{"derivedFrom":makeQuery(id+"F2.opPattern","COPY",BODY,{"derivedFrom":makeQuery(id+"F1.opRevolve","SWEPT_BODY",BODY,{"disambiguationData":[OSD([sQuery(id+"F0.wireOp",EDGE,"E1")])]}),"instanceName":"1"}),"instanceName":"1"}),"instanceName":"1"}),"instanceName":"1"}),"instanceName":"1"}),"instanceName":"1"});
            var Q710;
            Q710=makeQuery(id+"F11.opPattern","COPY",BODY,{"derivedFrom":makeQuery(id+"F10.opPattern","COPY",BODY,{"derivedFrom":makeQuery(id+"F9.opPattern","COPY",BODY,{"derivedFrom":makeQuery(id+"F7.opPattern","COPY",BODY,{"derivedFrom":makeQuery(id+"F6.opPattern","COPY",BODY,{"derivedFrom":makeQuery(id+"F3.opPattern","COPY",BODY,{"derivedFrom":makeQuery(id+"F2.opPattern","COPY",BODY,{"derivedFrom":makeQuery(id+"F1.opRevolve","SWEPT_BODY",BODY,{"disambiguationData":[OSD([sQuery(id+"F0.wireOp",EDGE,"E1")])]}),"instanceName":"1"}),"instanceName":"1"}),"instanceName":"1"}),"instanceName":"1"}),"instanceName":"1"}),"instanceName":"1"}),"instanceName":"1"});
            var Q711;
            Q711=makeQuery(id+"F11.opPattern","COPY",BODY,{"derivedFrom":makeQuery(id+"F10.opPattern","COPY",BODY,{"derivedFrom":makeQuery(id+"F9.opPattern","COPY",BODY,{"derivedFrom":makeQuery(id+"F7.opPattern","COPY",BODY,{"derivedFrom":makeQuery(id+"F6.opPattern","COPY",BODY,{"derivedFrom":makeQuery(id+"F4.opPattern","COPY",BODY,{"derivedFrom":makeQuery(id+"F1.opRevolve","SWEPT_BODY",BODY,{"disambiguationData":[OSD([sQuery(id+"F0.wireOp",EDGE,"E1")])]}),"instanceName":"1"}),"instanceName":"1"}),"instanceName":"1"}),"instanceName":"1"}),"instanceName":"1"}),"instanceName":"1"});
            var Q712;
            Q712=makeQuery(id+"F11.opPattern","COPY",BODY,{"derivedFrom":makeQuery(id+"F10.opPattern","COPY",BODY,{"derivedFrom":makeQuery(id+"F9.opPattern","COPY",BODY,{"derivedFrom":makeQuery(id+"F7.opPattern","COPY",BODY,{"derivedFrom":makeQuery(id+"F6.opPattern","COPY",BODY,{"derivedFrom":makeQuery(id+"F4.opPattern","COPY",BODY,{"derivedFrom":makeQuery(id+"F2.opPattern","COPY",BODY,{"derivedFrom":makeQuery(id+"F1.opRevolve","SWEPT_BODY",BODY,{"disambiguationData":[OSD([sQuery(id+"F0.wireOp",EDGE,"E1")])]}),"instanceName":"1"}),"instanceName":"1"}),"instanceName":"1"}),"instanceName":"1"}),"instanceName":"1"}),"instanceName":"1"}),"instanceName":"1"});
            var Q713;
            Q713=makeQuery(id+"F11.opPattern","COPY",BODY,{"derivedFrom":makeQuery(id+"F10.opPattern","COPY",BODY,{"derivedFrom":makeQuery(id+"F9.opPattern","COPY",BODY,{"derivedFrom":makeQuery(id+"F7.opPattern","COPY",BODY,{"derivedFrom":makeQuery(id+"F6.opPattern","COPY",BODY,{"derivedFrom":makeQuery(id+"F4.opPattern","COPY",BODY,{"derivedFrom":makeQuery(id+"F3.opPattern","COPY",BODY,{"derivedFrom":makeQuery(id+"F2.opPattern","COPY",BODY,{"derivedFrom":makeQuery(id+"F1.opRevolve","SWEPT_BODY",BODY,{"disambiguationData":[OSD([sQuery(id+"F0.wireOp",EDGE,"E1")])]}),"instanceName":"1"}),"instanceName":"1"}),"instanceName":"1"}),"instanceName":"1"}),"instanceName":"1"}),"instanceName":"1"}),"instanceName":"1"}),"instanceName":"1"});
            var Q714;
            Q714=makeQuery(id+"F11.opPattern","COPY",BODY,{"derivedFrom":makeQuery(id+"F10.opPattern","COPY",BODY,{"derivedFrom":makeQuery(id+"F9.opPattern","COPY",BODY,{"derivedFrom":makeQuery(id+"F7.opPattern","COPY",BODY,{"derivedFrom":makeQuery(id+"F6.opPattern","COPY",BODY,{"derivedFrom":makeQuery(id+"F5.opPattern","COPY",BODY,{"derivedFrom":makeQuery(id+"F1.opRevolve","SWEPT_BODY",BODY,{"disambiguationData":[OSD([sQuery(id+"F0.wireOp",EDGE,"E1")])]}),"instanceName":"1"}),"instanceName":"1"}),"instanceName":"1"}),"instanceName":"1"}),"instanceName":"1"}),"instanceName":"1"});
            var Q715;
            Q715=makeQuery(id+"F11.opPattern","COPY",BODY,{"derivedFrom":makeQuery(id+"F10.opPattern","COPY",BODY,{"derivedFrom":makeQuery(id+"F9.opPattern","COPY",BODY,{"derivedFrom":makeQuery(id+"F7.opPattern","COPY",BODY,{"derivedFrom":makeQuery(id+"F6.opPattern","COPY",BODY,{"derivedFrom":makeQuery(id+"F5.opPattern","COPY",BODY,{"derivedFrom":makeQuery(id+"F2.opPattern","COPY",BODY,{"derivedFrom":makeQuery(id+"F1.opRevolve","SWEPT_BODY",BODY,{"disambiguationData":[OSD([sQuery(id+"F0.wireOp",EDGE,"E1")])]}),"instanceName":"1"}),"instanceName":"1"}),"instanceName":"1"}),"instanceName":"1"}),"instanceName":"1"}),"instanceName":"1"}),"instanceName":"1"});
            var Q716;
            Q716=makeQuery(id+"F11.opPattern","COPY",BODY,{"derivedFrom":makeQuery(id+"F10.opPattern","COPY",BODY,{"derivedFrom":makeQuery(id+"F9.opPattern","COPY",BODY,{"derivedFrom":makeQuery(id+"F7.opPattern","COPY",BODY,{"derivedFrom":makeQuery(id+"F6.opPattern","COPY",BODY,{"derivedFrom":makeQuery(id+"F5.opPattern","COPY",BODY,{"derivedFrom":makeQuery(id+"F3.opPattern","COPY",BODY,{"derivedFrom":makeQuery(id+"F2.opPattern","COPY",BODY,{"derivedFrom":makeQuery(id+"F1.opRevolve","SWEPT_BODY",BODY,{"disambiguationData":[OSD([sQuery(id+"F0.wireOp",EDGE,"E1")])]}),"instanceName":"1"}),"instanceName":"1"}),"instanceName":"1"}),"instanceName":"1"}),"instanceName":"1"}),"instanceName":"1"}),"instanceName":"1"}),"instanceName":"1"});
            var Q717;
            Q717=makeQuery(id+"F11.opPattern","COPY",BODY,{"derivedFrom":makeQuery(id+"F10.opPattern","COPY",BODY,{"derivedFrom":makeQuery(id+"F9.opPattern","COPY",BODY,{"derivedFrom":makeQuery(id+"F7.opPattern","COPY",BODY,{"derivedFrom":makeQuery(id+"F6.opPattern","COPY",BODY,{"derivedFrom":makeQuery(id+"F5.opPattern","COPY",BODY,{"derivedFrom":makeQuery(id+"F4.opPattern","COPY",BODY,{"derivedFrom":makeQuery(id+"F1.opRevolve","SWEPT_BODY",BODY,{"disambiguationData":[OSD([sQuery(id+"F0.wireOp",EDGE,"E1")])]}),"instanceName":"1"}),"instanceName":"1"}),"instanceName":"1"}),"instanceName":"1"}),"instanceName":"1"}),"instanceName":"1"}),"instanceName":"1"});
            var Q718;
            Q718=makeQuery(id+"F11.opPattern","COPY",BODY,{"derivedFrom":makeQuery(id+"F10.opPattern","COPY",BODY,{"derivedFrom":makeQuery(id+"F9.opPattern","COPY",BODY,{"derivedFrom":makeQuery(id+"F7.opPattern","COPY",BODY,{"derivedFrom":makeQuery(id+"F6.opPattern","COPY",BODY,{"derivedFrom":makeQuery(id+"F5.opPattern","COPY",BODY,{"derivedFrom":makeQuery(id+"F4.opPattern","COPY",BODY,{"derivedFrom":makeQuery(id+"F2.opPattern","COPY",BODY,{"derivedFrom":makeQuery(id+"F1.opRevolve","SWEPT_BODY",BODY,{"disambiguationData":[OSD([sQuery(id+"F0.wireOp",EDGE,"E1")])]}),"instanceName":"1"}),"instanceName":"1"}),"instanceName":"1"}),"instanceName":"1"}),"instanceName":"1"}),"instanceName":"1"}),"instanceName":"1"}),"instanceName":"1"});
            var Q719;
            Q719=makeQuery(id+"F11.opPattern","COPY",BODY,{"derivedFrom":makeQuery(id+"F10.opPattern","COPY",BODY,{"derivedFrom":makeQuery(id+"F9.opPattern","COPY",BODY,{"derivedFrom":makeQuery(id+"F7.opPattern","COPY",BODY,{"derivedFrom":makeQuery(id+"F6.opPattern","COPY",BODY,{"derivedFrom":makeQuery(id+"F5.opPattern","COPY",BODY,{"derivedFrom":makeQuery(id+"F4.opPattern","COPY",BODY,{"derivedFrom":makeQuery(id+"F3.opPattern","COPY",BODY,{"derivedFrom":makeQuery(id+"F2.opPattern","COPY",BODY,{"derivedFrom":makeQuery(id+"F1.opRevolve","SWEPT_BODY",BODY,{"disambiguationData":[OSD([sQuery(id+"F0.wireOp",EDGE,"E1")])]}),"instanceName":"1"}),"instanceName":"1"}),"instanceName":"1"}),"instanceName":"1"}),"instanceName":"1"}),"instanceName":"1"}),"instanceName":"1"}),"instanceName":"1"}),"instanceName":"1"});
            var Q720;
            Q720=makeQuery(id+"F11.opPattern","COPY",BODY,{"derivedFrom":makeQuery(id+"F10.opPattern","COPY",BODY,{"derivedFrom":makeQuery(id+"F9.opPattern","COPY",BODY,{"derivedFrom":makeQuery(id+"F8.opPattern","COPY",BODY,{"derivedFrom":makeQuery(id+"F1.opRevolve","SWEPT_BODY",BODY,{"disambiguationData":[OSD([sQuery(id+"F0.wireOp",EDGE,"E1")])]}),"instanceName":"1"}),"instanceName":"1"}),"instanceName":"1"}),"instanceName":"1"});
            var Q721;
            Q721=makeQuery(id+"F11.opPattern","COPY",BODY,{"derivedFrom":makeQuery(id+"F10.opPattern","COPY",BODY,{"derivedFrom":makeQuery(id+"F9.opPattern","COPY",BODY,{"derivedFrom":makeQuery(id+"F8.opPattern","COPY",BODY,{"derivedFrom":makeQuery(id+"F2.opPattern","COPY",BODY,{"derivedFrom":makeQuery(id+"F1.opRevolve","SWEPT_BODY",BODY,{"disambiguationData":[OSD([sQuery(id+"F0.wireOp",EDGE,"E1")])]}),"instanceName":"1"}),"instanceName":"1"}),"instanceName":"1"}),"instanceName":"1"}),"instanceName":"1"});
            var Q722;
            Q722=makeQuery(id+"F11.opPattern","COPY",BODY,{"derivedFrom":makeQuery(id+"F10.opPattern","COPY",BODY,{"derivedFrom":makeQuery(id+"F9.opPattern","COPY",BODY,{"derivedFrom":makeQuery(id+"F8.opPattern","COPY",BODY,{"derivedFrom":makeQuery(id+"F3.opPattern","COPY",BODY,{"derivedFrom":makeQuery(id+"F2.opPattern","COPY",BODY,{"derivedFrom":makeQuery(id+"F1.opRevolve","SWEPT_BODY",BODY,{"disambiguationData":[OSD([sQuery(id+"F0.wireOp",EDGE,"E1")])]}),"instanceName":"1"}),"instanceName":"1"}),"instanceName":"1"}),"instanceName":"1"}),"instanceName":"1"}),"instanceName":"1"});
            var Q723;
            Q723=makeQuery(id+"F11.opPattern","COPY",BODY,{"derivedFrom":makeQuery(id+"F10.opPattern","COPY",BODY,{"derivedFrom":makeQuery(id+"F9.opPattern","COPY",BODY,{"derivedFrom":makeQuery(id+"F8.opPattern","COPY",BODY,{"derivedFrom":makeQuery(id+"F4.opPattern","COPY",BODY,{"derivedFrom":makeQuery(id+"F1.opRevolve","SWEPT_BODY",BODY,{"disambiguationData":[OSD([sQuery(id+"F0.wireOp",EDGE,"E1")])]}),"instanceName":"1"}),"instanceName":"1"}),"instanceName":"1"}),"instanceName":"1"}),"instanceName":"1"});
            var Q724;
            Q724=makeQuery(id+"F11.opPattern","COPY",BODY,{"derivedFrom":makeQuery(id+"F10.opPattern","COPY",BODY,{"derivedFrom":makeQuery(id+"F9.opPattern","COPY",BODY,{"derivedFrom":makeQuery(id+"F8.opPattern","COPY",BODY,{"derivedFrom":makeQuery(id+"F4.opPattern","COPY",BODY,{"derivedFrom":makeQuery(id+"F2.opPattern","COPY",BODY,{"derivedFrom":makeQuery(id+"F1.opRevolve","SWEPT_BODY",BODY,{"disambiguationData":[OSD([sQuery(id+"F0.wireOp",EDGE,"E1")])]}),"instanceName":"1"}),"instanceName":"1"}),"instanceName":"1"}),"instanceName":"1"}),"instanceName":"1"}),"instanceName":"1"});
            var Q725;
            Q725=makeQuery(id+"F11.opPattern","COPY",BODY,{"derivedFrom":makeQuery(id+"F10.opPattern","COPY",BODY,{"derivedFrom":makeQuery(id+"F9.opPattern","COPY",BODY,{"derivedFrom":makeQuery(id+"F8.opPattern","COPY",BODY,{"derivedFrom":makeQuery(id+"F4.opPattern","COPY",BODY,{"derivedFrom":makeQuery(id+"F3.opPattern","COPY",BODY,{"derivedFrom":makeQuery(id+"F2.opPattern","COPY",BODY,{"derivedFrom":makeQuery(id+"F1.opRevolve","SWEPT_BODY",BODY,{"disambiguationData":[OSD([sQuery(id+"F0.wireOp",EDGE,"E1")])]}),"instanceName":"1"}),"instanceName":"1"}),"instanceName":"1"}),"instanceName":"1"}),"instanceName":"1"}),"instanceName":"1"}),"instanceName":"1"});
            var Q726;
            Q726=makeQuery(id+"F11.opPattern","COPY",BODY,{"derivedFrom":makeQuery(id+"F10.opPattern","COPY",BODY,{"derivedFrom":makeQuery(id+"F9.opPattern","COPY",BODY,{"derivedFrom":makeQuery(id+"F8.opPattern","COPY",BODY,{"derivedFrom":makeQuery(id+"F5.opPattern","COPY",BODY,{"derivedFrom":makeQuery(id+"F1.opRevolve","SWEPT_BODY",BODY,{"disambiguationData":[OSD([sQuery(id+"F0.wireOp",EDGE,"E1")])]}),"instanceName":"1"}),"instanceName":"1"}),"instanceName":"1"}),"instanceName":"1"}),"instanceName":"1"});
            var Q727;
            Q727=makeQuery(id+"F11.opPattern","COPY",BODY,{"derivedFrom":makeQuery(id+"F10.opPattern","COPY",BODY,{"derivedFrom":makeQuery(id+"F9.opPattern","COPY",BODY,{"derivedFrom":makeQuery(id+"F8.opPattern","COPY",BODY,{"derivedFrom":makeQuery(id+"F5.opPattern","COPY",BODY,{"derivedFrom":makeQuery(id+"F2.opPattern","COPY",BODY,{"derivedFrom":makeQuery(id+"F1.opRevolve","SWEPT_BODY",BODY,{"disambiguationData":[OSD([sQuery(id+"F0.wireOp",EDGE,"E1")])]}),"instanceName":"1"}),"instanceName":"1"}),"instanceName":"1"}),"instanceName":"1"}),"instanceName":"1"}),"instanceName":"1"});
            var Q728;
            Q728=makeQuery(id+"F11.opPattern","COPY",BODY,{"derivedFrom":makeQuery(id+"F10.opPattern","COPY",BODY,{"derivedFrom":makeQuery(id+"F9.opPattern","COPY",BODY,{"derivedFrom":makeQuery(id+"F8.opPattern","COPY",BODY,{"derivedFrom":makeQuery(id+"F5.opPattern","COPY",BODY,{"derivedFrom":makeQuery(id+"F3.opPattern","COPY",BODY,{"derivedFrom":makeQuery(id+"F2.opPattern","COPY",BODY,{"derivedFrom":makeQuery(id+"F1.opRevolve","SWEPT_BODY",BODY,{"disambiguationData":[OSD([sQuery(id+"F0.wireOp",EDGE,"E1")])]}),"instanceName":"1"}),"instanceName":"1"}),"instanceName":"1"}),"instanceName":"1"}),"instanceName":"1"}),"instanceName":"1"}),"instanceName":"1"});
            var Q729;
            Q729=makeQuery(id+"F11.opPattern","COPY",BODY,{"derivedFrom":makeQuery(id+"F10.opPattern","COPY",BODY,{"derivedFrom":makeQuery(id+"F9.opPattern","COPY",BODY,{"derivedFrom":makeQuery(id+"F8.opPattern","COPY",BODY,{"derivedFrom":makeQuery(id+"F5.opPattern","COPY",BODY,{"derivedFrom":makeQuery(id+"F4.opPattern","COPY",BODY,{"derivedFrom":makeQuery(id+"F1.opRevolve","SWEPT_BODY",BODY,{"disambiguationData":[OSD([sQuery(id+"F0.wireOp",EDGE,"E1")])]}),"instanceName":"1"}),"instanceName":"1"}),"instanceName":"1"}),"instanceName":"1"}),"instanceName":"1"}),"instanceName":"1"});
            var Q730;
            Q730=makeQuery(id+"F11.opPattern","COPY",BODY,{"derivedFrom":makeQuery(id+"F10.opPattern","COPY",BODY,{"derivedFrom":makeQuery(id+"F9.opPattern","COPY",BODY,{"derivedFrom":makeQuery(id+"F8.opPattern","COPY",BODY,{"derivedFrom":makeQuery(id+"F5.opPattern","COPY",BODY,{"derivedFrom":makeQuery(id+"F4.opPattern","COPY",BODY,{"derivedFrom":makeQuery(id+"F2.opPattern","COPY",BODY,{"derivedFrom":makeQuery(id+"F1.opRevolve","SWEPT_BODY",BODY,{"disambiguationData":[OSD([sQuery(id+"F0.wireOp",EDGE,"E1")])]}),"instanceName":"1"}),"instanceName":"1"}),"instanceName":"1"}),"instanceName":"1"}),"instanceName":"1"}),"instanceName":"1"}),"instanceName":"1"});
            var Q731;
            Q731=makeQuery(id+"F11.opPattern","COPY",BODY,{"derivedFrom":makeQuery(id+"F10.opPattern","COPY",BODY,{"derivedFrom":makeQuery(id+"F9.opPattern","COPY",BODY,{"derivedFrom":makeQuery(id+"F8.opPattern","COPY",BODY,{"derivedFrom":makeQuery(id+"F5.opPattern","COPY",BODY,{"derivedFrom":makeQuery(id+"F4.opPattern","COPY",BODY,{"derivedFrom":makeQuery(id+"F3.opPattern","COPY",BODY,{"derivedFrom":makeQuery(id+"F2.opPattern","COPY",BODY,{"derivedFrom":makeQuery(id+"F1.opRevolve","SWEPT_BODY",BODY,{"disambiguationData":[OSD([sQuery(id+"F0.wireOp",EDGE,"E1")])]}),"instanceName":"1"}),"instanceName":"1"}),"instanceName":"1"}),"instanceName":"1"}),"instanceName":"1"}),"instanceName":"1"}),"instanceName":"1"}),"instanceName":"1"});
            var Q732;
            Q732=makeQuery(id+"F11.opPattern","COPY",BODY,{"derivedFrom":makeQuery(id+"F10.opPattern","COPY",BODY,{"derivedFrom":makeQuery(id+"F9.opPattern","COPY",BODY,{"derivedFrom":makeQuery(id+"F8.opPattern","COPY",BODY,{"derivedFrom":makeQuery(id+"F6.opPattern","COPY",BODY,{"derivedFrom":makeQuery(id+"F1.opRevolve","SWEPT_BODY",BODY,{"disambiguationData":[OSD([sQuery(id+"F0.wireOp",EDGE,"E1")])]}),"instanceName":"1"}),"instanceName":"1"}),"instanceName":"1"}),"instanceName":"1"}),"instanceName":"1"});
            var Q733;
            Q733=makeQuery(id+"F11.opPattern","COPY",BODY,{"derivedFrom":makeQuery(id+"F10.opPattern","COPY",BODY,{"derivedFrom":makeQuery(id+"F9.opPattern","COPY",BODY,{"derivedFrom":makeQuery(id+"F8.opPattern","COPY",BODY,{"derivedFrom":makeQuery(id+"F6.opPattern","COPY",BODY,{"derivedFrom":makeQuery(id+"F2.opPattern","COPY",BODY,{"derivedFrom":makeQuery(id+"F1.opRevolve","SWEPT_BODY",BODY,{"disambiguationData":[OSD([sQuery(id+"F0.wireOp",EDGE,"E1")])]}),"instanceName":"1"}),"instanceName":"1"}),"instanceName":"1"}),"instanceName":"1"}),"instanceName":"1"}),"instanceName":"1"});
            var Q734;
            Q734=makeQuery(id+"F11.opPattern","COPY",BODY,{"derivedFrom":makeQuery(id+"F10.opPattern","COPY",BODY,{"derivedFrom":makeQuery(id+"F9.opPattern","COPY",BODY,{"derivedFrom":makeQuery(id+"F8.opPattern","COPY",BODY,{"derivedFrom":makeQuery(id+"F6.opPattern","COPY",BODY,{"derivedFrom":makeQuery(id+"F3.opPattern","COPY",BODY,{"derivedFrom":makeQuery(id+"F2.opPattern","COPY",BODY,{"derivedFrom":makeQuery(id+"F1.opRevolve","SWEPT_BODY",BODY,{"disambiguationData":[OSD([sQuery(id+"F0.wireOp",EDGE,"E1")])]}),"instanceName":"1"}),"instanceName":"1"}),"instanceName":"1"}),"instanceName":"1"}),"instanceName":"1"}),"instanceName":"1"}),"instanceName":"1"});
            var Q735;
            Q735=makeQuery(id+"F11.opPattern","COPY",BODY,{"derivedFrom":makeQuery(id+"F10.opPattern","COPY",BODY,{"derivedFrom":makeQuery(id+"F9.opPattern","COPY",BODY,{"derivedFrom":makeQuery(id+"F8.opPattern","COPY",BODY,{"derivedFrom":makeQuery(id+"F6.opPattern","COPY",BODY,{"derivedFrom":makeQuery(id+"F4.opPattern","COPY",BODY,{"derivedFrom":makeQuery(id+"F1.opRevolve","SWEPT_BODY",BODY,{"disambiguationData":[OSD([sQuery(id+"F0.wireOp",EDGE,"E1")])]}),"instanceName":"1"}),"instanceName":"1"}),"instanceName":"1"}),"instanceName":"1"}),"instanceName":"1"}),"instanceName":"1"});
            var Q736;
            Q736=makeQuery(id+"F11.opPattern","COPY",BODY,{"derivedFrom":makeQuery(id+"F10.opPattern","COPY",BODY,{"derivedFrom":makeQuery(id+"F9.opPattern","COPY",BODY,{"derivedFrom":makeQuery(id+"F8.opPattern","COPY",BODY,{"derivedFrom":makeQuery(id+"F6.opPattern","COPY",BODY,{"derivedFrom":makeQuery(id+"F4.opPattern","COPY",BODY,{"derivedFrom":makeQuery(id+"F2.opPattern","COPY",BODY,{"derivedFrom":makeQuery(id+"F1.opRevolve","SWEPT_BODY",BODY,{"disambiguationData":[OSD([sQuery(id+"F0.wireOp",EDGE,"E1")])]}),"instanceName":"1"}),"instanceName":"1"}),"instanceName":"1"}),"instanceName":"1"}),"instanceName":"1"}),"instanceName":"1"}),"instanceName":"1"});
            var Q737;
            Q737=makeQuery(id+"F11.opPattern","COPY",BODY,{"derivedFrom":makeQuery(id+"F10.opPattern","COPY",BODY,{"derivedFrom":makeQuery(id+"F9.opPattern","COPY",BODY,{"derivedFrom":makeQuery(id+"F8.opPattern","COPY",BODY,{"derivedFrom":makeQuery(id+"F6.opPattern","COPY",BODY,{"derivedFrom":makeQuery(id+"F4.opPattern","COPY",BODY,{"derivedFrom":makeQuery(id+"F3.opPattern","COPY",BODY,{"derivedFrom":makeQuery(id+"F2.opPattern","COPY",BODY,{"derivedFrom":makeQuery(id+"F1.opRevolve","SWEPT_BODY",BODY,{"disambiguationData":[OSD([sQuery(id+"F0.wireOp",EDGE,"E1")])]}),"instanceName":"1"}),"instanceName":"1"}),"instanceName":"1"}),"instanceName":"1"}),"instanceName":"1"}),"instanceName":"1"}),"instanceName":"1"}),"instanceName":"1"});
            var Q738;
            Q738=makeQuery(id+"F11.opPattern","COPY",BODY,{"derivedFrom":makeQuery(id+"F10.opPattern","COPY",BODY,{"derivedFrom":makeQuery(id+"F9.opPattern","COPY",BODY,{"derivedFrom":makeQuery(id+"F8.opPattern","COPY",BODY,{"derivedFrom":makeQuery(id+"F6.opPattern","COPY",BODY,{"derivedFrom":makeQuery(id+"F5.opPattern","COPY",BODY,{"derivedFrom":makeQuery(id+"F1.opRevolve","SWEPT_BODY",BODY,{"disambiguationData":[OSD([sQuery(id+"F0.wireOp",EDGE,"E1")])]}),"instanceName":"1"}),"instanceName":"1"}),"instanceName":"1"}),"instanceName":"1"}),"instanceName":"1"}),"instanceName":"1"});
            var Q739;
            Q739=makeQuery(id+"F11.opPattern","COPY",BODY,{"derivedFrom":makeQuery(id+"F10.opPattern","COPY",BODY,{"derivedFrom":makeQuery(id+"F9.opPattern","COPY",BODY,{"derivedFrom":makeQuery(id+"F8.opPattern","COPY",BODY,{"derivedFrom":makeQuery(id+"F6.opPattern","COPY",BODY,{"derivedFrom":makeQuery(id+"F5.opPattern","COPY",BODY,{"derivedFrom":makeQuery(id+"F2.opPattern","COPY",BODY,{"derivedFrom":makeQuery(id+"F1.opRevolve","SWEPT_BODY",BODY,{"disambiguationData":[OSD([sQuery(id+"F0.wireOp",EDGE,"E1")])]}),"instanceName":"1"}),"instanceName":"1"}),"instanceName":"1"}),"instanceName":"1"}),"instanceName":"1"}),"instanceName":"1"}),"instanceName":"1"});
            var Q740;
            Q740=makeQuery(id+"F11.opPattern","COPY",BODY,{"derivedFrom":makeQuery(id+"F10.opPattern","COPY",BODY,{"derivedFrom":makeQuery(id+"F9.opPattern","COPY",BODY,{"derivedFrom":makeQuery(id+"F8.opPattern","COPY",BODY,{"derivedFrom":makeQuery(id+"F6.opPattern","COPY",BODY,{"derivedFrom":makeQuery(id+"F5.opPattern","COPY",BODY,{"derivedFrom":makeQuery(id+"F3.opPattern","COPY",BODY,{"derivedFrom":makeQuery(id+"F2.opPattern","COPY",BODY,{"derivedFrom":makeQuery(id+"F1.opRevolve","SWEPT_BODY",BODY,{"disambiguationData":[OSD([sQuery(id+"F0.wireOp",EDGE,"E1")])]}),"instanceName":"1"}),"instanceName":"1"}),"instanceName":"1"}),"instanceName":"1"}),"instanceName":"1"}),"instanceName":"1"}),"instanceName":"1"}),"instanceName":"1"});
            var Q741;
            Q741=makeQuery(id+"F11.opPattern","COPY",BODY,{"derivedFrom":makeQuery(id+"F10.opPattern","COPY",BODY,{"derivedFrom":makeQuery(id+"F9.opPattern","COPY",BODY,{"derivedFrom":makeQuery(id+"F8.opPattern","COPY",BODY,{"derivedFrom":makeQuery(id+"F6.opPattern","COPY",BODY,{"derivedFrom":makeQuery(id+"F5.opPattern","COPY",BODY,{"derivedFrom":makeQuery(id+"F4.opPattern","COPY",BODY,{"derivedFrom":makeQuery(id+"F1.opRevolve","SWEPT_BODY",BODY,{"disambiguationData":[OSD([sQuery(id+"F0.wireOp",EDGE,"E1")])]}),"instanceName":"1"}),"instanceName":"1"}),"instanceName":"1"}),"instanceName":"1"}),"instanceName":"1"}),"instanceName":"1"}),"instanceName":"1"});
            var Q742;
            Q742=makeQuery(id+"F11.opPattern","COPY",BODY,{"derivedFrom":makeQuery(id+"F10.opPattern","COPY",BODY,{"derivedFrom":makeQuery(id+"F9.opPattern","COPY",BODY,{"derivedFrom":makeQuery(id+"F8.opPattern","COPY",BODY,{"derivedFrom":makeQuery(id+"F6.opPattern","COPY",BODY,{"derivedFrom":makeQuery(id+"F5.opPattern","COPY",BODY,{"derivedFrom":makeQuery(id+"F4.opPattern","COPY",BODY,{"derivedFrom":makeQuery(id+"F2.opPattern","COPY",BODY,{"derivedFrom":makeQuery(id+"F1.opRevolve","SWEPT_BODY",BODY,{"disambiguationData":[OSD([sQuery(id+"F0.wireOp",EDGE,"E1")])]}),"instanceName":"1"}),"instanceName":"1"}),"instanceName":"1"}),"instanceName":"1"}),"instanceName":"1"}),"instanceName":"1"}),"instanceName":"1"}),"instanceName":"1"});
            var Q743;
            Q743=makeQuery(id+"F11.opPattern","COPY",BODY,{"derivedFrom":makeQuery(id+"F10.opPattern","COPY",BODY,{"derivedFrom":makeQuery(id+"F9.opPattern","COPY",BODY,{"derivedFrom":makeQuery(id+"F8.opPattern","COPY",BODY,{"derivedFrom":makeQuery(id+"F6.opPattern","COPY",BODY,{"derivedFrom":makeQuery(id+"F5.opPattern","COPY",BODY,{"derivedFrom":makeQuery(id+"F4.opPattern","COPY",BODY,{"derivedFrom":makeQuery(id+"F3.opPattern","COPY",BODY,{"derivedFrom":makeQuery(id+"F2.opPattern","COPY",BODY,{"derivedFrom":makeQuery(id+"F1.opRevolve","SWEPT_BODY",BODY,{"disambiguationData":[OSD([sQuery(id+"F0.wireOp",EDGE,"E1")])]}),"instanceName":"1"}),"instanceName":"1"}),"instanceName":"1"}),"instanceName":"1"}),"instanceName":"1"}),"instanceName":"1"}),"instanceName":"1"}),"instanceName":"1"}),"instanceName":"1"});
            var Q744;
            Q744=makeQuery(id+"F11.opPattern","COPY",BODY,{"derivedFrom":makeQuery(id+"F10.opPattern","COPY",BODY,{"derivedFrom":makeQuery(id+"F9.opPattern","COPY",BODY,{"derivedFrom":makeQuery(id+"F8.opPattern","COPY",BODY,{"derivedFrom":makeQuery(id+"F7.opPattern","COPY",BODY,{"derivedFrom":makeQuery(id+"F1.opRevolve","SWEPT_BODY",BODY,{"disambiguationData":[OSD([sQuery(id+"F0.wireOp",EDGE,"E1")])]}),"instanceName":"1"}),"instanceName":"1"}),"instanceName":"1"}),"instanceName":"1"}),"instanceName":"1"});
            var Q745;
            Q745=makeQuery(id+"F11.opPattern","COPY",BODY,{"derivedFrom":makeQuery(id+"F10.opPattern","COPY",BODY,{"derivedFrom":makeQuery(id+"F9.opPattern","COPY",BODY,{"derivedFrom":makeQuery(id+"F8.opPattern","COPY",BODY,{"derivedFrom":makeQuery(id+"F7.opPattern","COPY",BODY,{"derivedFrom":makeQuery(id+"F2.opPattern","COPY",BODY,{"derivedFrom":makeQuery(id+"F1.opRevolve","SWEPT_BODY",BODY,{"disambiguationData":[OSD([sQuery(id+"F0.wireOp",EDGE,"E1")])]}),"instanceName":"1"}),"instanceName":"1"}),"instanceName":"1"}),"instanceName":"1"}),"instanceName":"1"}),"instanceName":"1"});
            var Q746;
            Q746=makeQuery(id+"F11.opPattern","COPY",BODY,{"derivedFrom":makeQuery(id+"F10.opPattern","COPY",BODY,{"derivedFrom":makeQuery(id+"F9.opPattern","COPY",BODY,{"derivedFrom":makeQuery(id+"F8.opPattern","COPY",BODY,{"derivedFrom":makeQuery(id+"F7.opPattern","COPY",BODY,{"derivedFrom":makeQuery(id+"F3.opPattern","COPY",BODY,{"derivedFrom":makeQuery(id+"F2.opPattern","COPY",BODY,{"derivedFrom":makeQuery(id+"F1.opRevolve","SWEPT_BODY",BODY,{"disambiguationData":[OSD([sQuery(id+"F0.wireOp",EDGE,"E1")])]}),"instanceName":"1"}),"instanceName":"1"}),"instanceName":"1"}),"instanceName":"1"}),"instanceName":"1"}),"instanceName":"1"}),"instanceName":"1"});
            var Q747;
            Q747=makeQuery(id+"F11.opPattern","COPY",BODY,{"derivedFrom":makeQuery(id+"F10.opPattern","COPY",BODY,{"derivedFrom":makeQuery(id+"F9.opPattern","COPY",BODY,{"derivedFrom":makeQuery(id+"F8.opPattern","COPY",BODY,{"derivedFrom":makeQuery(id+"F7.opPattern","COPY",BODY,{"derivedFrom":makeQuery(id+"F4.opPattern","COPY",BODY,{"derivedFrom":makeQuery(id+"F1.opRevolve","SWEPT_BODY",BODY,{"disambiguationData":[OSD([sQuery(id+"F0.wireOp",EDGE,"E1")])]}),"instanceName":"1"}),"instanceName":"1"}),"instanceName":"1"}),"instanceName":"1"}),"instanceName":"1"}),"instanceName":"1"});
            var Q748;
            Q748=makeQuery(id+"F11.opPattern","COPY",BODY,{"derivedFrom":makeQuery(id+"F10.opPattern","COPY",BODY,{"derivedFrom":makeQuery(id+"F9.opPattern","COPY",BODY,{"derivedFrom":makeQuery(id+"F8.opPattern","COPY",BODY,{"derivedFrom":makeQuery(id+"F7.opPattern","COPY",BODY,{"derivedFrom":makeQuery(id+"F4.opPattern","COPY",BODY,{"derivedFrom":makeQuery(id+"F2.opPattern","COPY",BODY,{"derivedFrom":makeQuery(id+"F1.opRevolve","SWEPT_BODY",BODY,{"disambiguationData":[OSD([sQuery(id+"F0.wireOp",EDGE,"E1")])]}),"instanceName":"1"}),"instanceName":"1"}),"instanceName":"1"}),"instanceName":"1"}),"instanceName":"1"}),"instanceName":"1"}),"instanceName":"1"});
            var Q749;
            Q749=makeQuery(id+"F11.opPattern","COPY",BODY,{"derivedFrom":makeQuery(id+"F10.opPattern","COPY",BODY,{"derivedFrom":makeQuery(id+"F9.opPattern","COPY",BODY,{"derivedFrom":makeQuery(id+"F8.opPattern","COPY",BODY,{"derivedFrom":makeQuery(id+"F7.opPattern","COPY",BODY,{"derivedFrom":makeQuery(id+"F4.opPattern","COPY",BODY,{"derivedFrom":makeQuery(id+"F3.opPattern","COPY",BODY,{"derivedFrom":makeQuery(id+"F2.opPattern","COPY",BODY,{"derivedFrom":makeQuery(id+"F1.opRevolve","SWEPT_BODY",BODY,{"disambiguationData":[OSD([sQuery(id+"F0.wireOp",EDGE,"E1")])]}),"instanceName":"1"}),"instanceName":"1"}),"instanceName":"1"}),"instanceName":"1"}),"instanceName":"1"}),"instanceName":"1"}),"instanceName":"1"}),"instanceName":"1"});
            var Q750;
            Q750=makeQuery(id+"F11.opPattern","COPY",BODY,{"derivedFrom":makeQuery(id+"F10.opPattern","COPY",BODY,{"derivedFrom":makeQuery(id+"F9.opPattern","COPY",BODY,{"derivedFrom":makeQuery(id+"F8.opPattern","COPY",BODY,{"derivedFrom":makeQuery(id+"F7.opPattern","COPY",BODY,{"derivedFrom":makeQuery(id+"F5.opPattern","COPY",BODY,{"derivedFrom":makeQuery(id+"F1.opRevolve","SWEPT_BODY",BODY,{"disambiguationData":[OSD([sQuery(id+"F0.wireOp",EDGE,"E1")])]}),"instanceName":"1"}),"instanceName":"1"}),"instanceName":"1"}),"instanceName":"1"}),"instanceName":"1"}),"instanceName":"1"});
            var Q751;
            Q751=makeQuery(id+"F11.opPattern","COPY",BODY,{"derivedFrom":makeQuery(id+"F10.opPattern","COPY",BODY,{"derivedFrom":makeQuery(id+"F9.opPattern","COPY",BODY,{"derivedFrom":makeQuery(id+"F8.opPattern","COPY",BODY,{"derivedFrom":makeQuery(id+"F7.opPattern","COPY",BODY,{"derivedFrom":makeQuery(id+"F5.opPattern","COPY",BODY,{"derivedFrom":makeQuery(id+"F2.opPattern","COPY",BODY,{"derivedFrom":makeQuery(id+"F1.opRevolve","SWEPT_BODY",BODY,{"disambiguationData":[OSD([sQuery(id+"F0.wireOp",EDGE,"E1")])]}),"instanceName":"1"}),"instanceName":"1"}),"instanceName":"1"}),"instanceName":"1"}),"instanceName":"1"}),"instanceName":"1"}),"instanceName":"1"});
            var Q752;
            Q752=makeQuery(id+"F11.opPattern","COPY",BODY,{"derivedFrom":makeQuery(id+"F10.opPattern","COPY",BODY,{"derivedFrom":makeQuery(id+"F9.opPattern","COPY",BODY,{"derivedFrom":makeQuery(id+"F8.opPattern","COPY",BODY,{"derivedFrom":makeQuery(id+"F7.opPattern","COPY",BODY,{"derivedFrom":makeQuery(id+"F5.opPattern","COPY",BODY,{"derivedFrom":makeQuery(id+"F3.opPattern","COPY",BODY,{"derivedFrom":makeQuery(id+"F2.opPattern","COPY",BODY,{"derivedFrom":makeQuery(id+"F1.opRevolve","SWEPT_BODY",BODY,{"disambiguationData":[OSD([sQuery(id+"F0.wireOp",EDGE,"E1")])]}),"instanceName":"1"}),"instanceName":"1"}),"instanceName":"1"}),"instanceName":"1"}),"instanceName":"1"}),"instanceName":"1"}),"instanceName":"1"}),"instanceName":"1"});
            var Q753;
            Q753=makeQuery(id+"F11.opPattern","COPY",BODY,{"derivedFrom":makeQuery(id+"F10.opPattern","COPY",BODY,{"derivedFrom":makeQuery(id+"F9.opPattern","COPY",BODY,{"derivedFrom":makeQuery(id+"F8.opPattern","COPY",BODY,{"derivedFrom":makeQuery(id+"F7.opPattern","COPY",BODY,{"derivedFrom":makeQuery(id+"F5.opPattern","COPY",BODY,{"derivedFrom":makeQuery(id+"F4.opPattern","COPY",BODY,{"derivedFrom":makeQuery(id+"F1.opRevolve","SWEPT_BODY",BODY,{"disambiguationData":[OSD([sQuery(id+"F0.wireOp",EDGE,"E1")])]}),"instanceName":"1"}),"instanceName":"1"}),"instanceName":"1"}),"instanceName":"1"}),"instanceName":"1"}),"instanceName":"1"}),"instanceName":"1"});
            var Q754;
            Q754=makeQuery(id+"F11.opPattern","COPY",BODY,{"derivedFrom":makeQuery(id+"F10.opPattern","COPY",BODY,{"derivedFrom":makeQuery(id+"F9.opPattern","COPY",BODY,{"derivedFrom":makeQuery(id+"F8.opPattern","COPY",BODY,{"derivedFrom":makeQuery(id+"F7.opPattern","COPY",BODY,{"derivedFrom":makeQuery(id+"F5.opPattern","COPY",BODY,{"derivedFrom":makeQuery(id+"F4.opPattern","COPY",BODY,{"derivedFrom":makeQuery(id+"F2.opPattern","COPY",BODY,{"derivedFrom":makeQuery(id+"F1.opRevolve","SWEPT_BODY",BODY,{"disambiguationData":[OSD([sQuery(id+"F0.wireOp",EDGE,"E1")])]}),"instanceName":"1"}),"instanceName":"1"}),"instanceName":"1"}),"instanceName":"1"}),"instanceName":"1"}),"instanceName":"1"}),"instanceName":"1"}),"instanceName":"1"});
            var Q755;
            Q755=makeQuery(id+"F11.opPattern","COPY",BODY,{"derivedFrom":makeQuery(id+"F10.opPattern","COPY",BODY,{"derivedFrom":makeQuery(id+"F9.opPattern","COPY",BODY,{"derivedFrom":makeQuery(id+"F8.opPattern","COPY",BODY,{"derivedFrom":makeQuery(id+"F7.opPattern","COPY",BODY,{"derivedFrom":makeQuery(id+"F5.opPattern","COPY",BODY,{"derivedFrom":makeQuery(id+"F4.opPattern","COPY",BODY,{"derivedFrom":makeQuery(id+"F3.opPattern","COPY",BODY,{"derivedFrom":makeQuery(id+"F2.opPattern","COPY",BODY,{"derivedFrom":makeQuery(id+"F1.opRevolve","SWEPT_BODY",BODY,{"disambiguationData":[OSD([sQuery(id+"F0.wireOp",EDGE,"E1")])]}),"instanceName":"1"}),"instanceName":"1"}),"instanceName":"1"}),"instanceName":"1"}),"instanceName":"1"}),"instanceName":"1"}),"instanceName":"1"}),"instanceName":"1"}),"instanceName":"1"});
            var Q756;
            Q756=makeQuery(id+"F11.opPattern","COPY",BODY,{"derivedFrom":makeQuery(id+"F10.opPattern","COPY",BODY,{"derivedFrom":makeQuery(id+"F9.opPattern","COPY",BODY,{"derivedFrom":makeQuery(id+"F8.opPattern","COPY",BODY,{"derivedFrom":makeQuery(id+"F7.opPattern","COPY",BODY,{"derivedFrom":makeQuery(id+"F6.opPattern","COPY",BODY,{"derivedFrom":makeQuery(id+"F1.opRevolve","SWEPT_BODY",BODY,{"disambiguationData":[OSD([sQuery(id+"F0.wireOp",EDGE,"E1")])]}),"instanceName":"1"}),"instanceName":"1"}),"instanceName":"1"}),"instanceName":"1"}),"instanceName":"1"}),"instanceName":"1"});
            var Q757;
            Q757=makeQuery(id+"F11.opPattern","COPY",BODY,{"derivedFrom":makeQuery(id+"F10.opPattern","COPY",BODY,{"derivedFrom":makeQuery(id+"F9.opPattern","COPY",BODY,{"derivedFrom":makeQuery(id+"F8.opPattern","COPY",BODY,{"derivedFrom":makeQuery(id+"F7.opPattern","COPY",BODY,{"derivedFrom":makeQuery(id+"F6.opPattern","COPY",BODY,{"derivedFrom":makeQuery(id+"F2.opPattern","COPY",BODY,{"derivedFrom":makeQuery(id+"F1.opRevolve","SWEPT_BODY",BODY,{"disambiguationData":[OSD([sQuery(id+"F0.wireOp",EDGE,"E1")])]}),"instanceName":"1"}),"instanceName":"1"}),"instanceName":"1"}),"instanceName":"1"}),"instanceName":"1"}),"instanceName":"1"}),"instanceName":"1"});
            var Q758;
            Q758=makeQuery(id+"F11.opPattern","COPY",BODY,{"derivedFrom":makeQuery(id+"F10.opPattern","COPY",BODY,{"derivedFrom":makeQuery(id+"F9.opPattern","COPY",BODY,{"derivedFrom":makeQuery(id+"F8.opPattern","COPY",BODY,{"derivedFrom":makeQuery(id+"F7.opPattern","COPY",BODY,{"derivedFrom":makeQuery(id+"F6.opPattern","COPY",BODY,{"derivedFrom":makeQuery(id+"F3.opPattern","COPY",BODY,{"derivedFrom":makeQuery(id+"F2.opPattern","COPY",BODY,{"derivedFrom":makeQuery(id+"F1.opRevolve","SWEPT_BODY",BODY,{"disambiguationData":[OSD([sQuery(id+"F0.wireOp",EDGE,"E1")])]}),"instanceName":"1"}),"instanceName":"1"}),"instanceName":"1"}),"instanceName":"1"}),"instanceName":"1"}),"instanceName":"1"}),"instanceName":"1"}),"instanceName":"1"});
            var Q759;
            Q759=makeQuery(id+"F11.opPattern","COPY",BODY,{"derivedFrom":makeQuery(id+"F10.opPattern","COPY",BODY,{"derivedFrom":makeQuery(id+"F9.opPattern","COPY",BODY,{"derivedFrom":makeQuery(id+"F8.opPattern","COPY",BODY,{"derivedFrom":makeQuery(id+"F7.opPattern","COPY",BODY,{"derivedFrom":makeQuery(id+"F6.opPattern","COPY",BODY,{"derivedFrom":makeQuery(id+"F4.opPattern","COPY",BODY,{"derivedFrom":makeQuery(id+"F1.opRevolve","SWEPT_BODY",BODY,{"disambiguationData":[OSD([sQuery(id+"F0.wireOp",EDGE,"E1")])]}),"instanceName":"1"}),"instanceName":"1"}),"instanceName":"1"}),"instanceName":"1"}),"instanceName":"1"}),"instanceName":"1"}),"instanceName":"1"});
            var Q760;
            Q760=makeQuery(id+"F11.opPattern","COPY",BODY,{"derivedFrom":makeQuery(id+"F10.opPattern","COPY",BODY,{"derivedFrom":makeQuery(id+"F9.opPattern","COPY",BODY,{"derivedFrom":makeQuery(id+"F8.opPattern","COPY",BODY,{"derivedFrom":makeQuery(id+"F7.opPattern","COPY",BODY,{"derivedFrom":makeQuery(id+"F6.opPattern","COPY",BODY,{"derivedFrom":makeQuery(id+"F4.opPattern","COPY",BODY,{"derivedFrom":makeQuery(id+"F2.opPattern","COPY",BODY,{"derivedFrom":makeQuery(id+"F1.opRevolve","SWEPT_BODY",BODY,{"disambiguationData":[OSD([sQuery(id+"F0.wireOp",EDGE,"E1")])]}),"instanceName":"1"}),"instanceName":"1"}),"instanceName":"1"}),"instanceName":"1"}),"instanceName":"1"}),"instanceName":"1"}),"instanceName":"1"}),"instanceName":"1"});
            var Q761;
            Q761=makeQuery(id+"F11.opPattern","COPY",BODY,{"derivedFrom":makeQuery(id+"F10.opPattern","COPY",BODY,{"derivedFrom":makeQuery(id+"F9.opPattern","COPY",BODY,{"derivedFrom":makeQuery(id+"F8.opPattern","COPY",BODY,{"derivedFrom":makeQuery(id+"F7.opPattern","COPY",BODY,{"derivedFrom":makeQuery(id+"F6.opPattern","COPY",BODY,{"derivedFrom":makeQuery(id+"F4.opPattern","COPY",BODY,{"derivedFrom":makeQuery(id+"F3.opPattern","COPY",BODY,{"derivedFrom":makeQuery(id+"F2.opPattern","COPY",BODY,{"derivedFrom":makeQuery(id+"F1.opRevolve","SWEPT_BODY",BODY,{"disambiguationData":[OSD([sQuery(id+"F0.wireOp",EDGE,"E1")])]}),"instanceName":"1"}),"instanceName":"1"}),"instanceName":"1"}),"instanceName":"1"}),"instanceName":"1"}),"instanceName":"1"}),"instanceName":"1"}),"instanceName":"1"}),"instanceName":"1"});
            var Q762;
            Q762=makeQuery(id+"F11.opPattern","COPY",BODY,{"derivedFrom":makeQuery(id+"F10.opPattern","COPY",BODY,{"derivedFrom":makeQuery(id+"F9.opPattern","COPY",BODY,{"derivedFrom":makeQuery(id+"F8.opPattern","COPY",BODY,{"derivedFrom":makeQuery(id+"F7.opPattern","COPY",BODY,{"derivedFrom":makeQuery(id+"F6.opPattern","COPY",BODY,{"derivedFrom":makeQuery(id+"F5.opPattern","COPY",BODY,{"derivedFrom":makeQuery(id+"F1.opRevolve","SWEPT_BODY",BODY,{"disambiguationData":[OSD([sQuery(id+"F0.wireOp",EDGE,"E1")])]}),"instanceName":"1"}),"instanceName":"1"}),"instanceName":"1"}),"instanceName":"1"}),"instanceName":"1"}),"instanceName":"1"}),"instanceName":"1"});
            var Q763;
            Q763=makeQuery(id+"F11.opPattern","COPY",BODY,{"derivedFrom":makeQuery(id+"F10.opPattern","COPY",BODY,{"derivedFrom":makeQuery(id+"F9.opPattern","COPY",BODY,{"derivedFrom":makeQuery(id+"F8.opPattern","COPY",BODY,{"derivedFrom":makeQuery(id+"F7.opPattern","COPY",BODY,{"derivedFrom":makeQuery(id+"F6.opPattern","COPY",BODY,{"derivedFrom":makeQuery(id+"F5.opPattern","COPY",BODY,{"derivedFrom":makeQuery(id+"F2.opPattern","COPY",BODY,{"derivedFrom":makeQuery(id+"F1.opRevolve","SWEPT_BODY",BODY,{"disambiguationData":[OSD([sQuery(id+"F0.wireOp",EDGE,"E1")])]}),"instanceName":"1"}),"instanceName":"1"}),"instanceName":"1"}),"instanceName":"1"}),"instanceName":"1"}),"instanceName":"1"}),"instanceName":"1"}),"instanceName":"1"});
            var Q764;
            Q764=makeQuery(id+"F11.opPattern","COPY",BODY,{"derivedFrom":makeQuery(id+"F10.opPattern","COPY",BODY,{"derivedFrom":makeQuery(id+"F9.opPattern","COPY",BODY,{"derivedFrom":makeQuery(id+"F8.opPattern","COPY",BODY,{"derivedFrom":makeQuery(id+"F7.opPattern","COPY",BODY,{"derivedFrom":makeQuery(id+"F6.opPattern","COPY",BODY,{"derivedFrom":makeQuery(id+"F5.opPattern","COPY",BODY,{"derivedFrom":makeQuery(id+"F3.opPattern","COPY",BODY,{"derivedFrom":makeQuery(id+"F2.opPattern","COPY",BODY,{"derivedFrom":makeQuery(id+"F1.opRevolve","SWEPT_BODY",BODY,{"disambiguationData":[OSD([sQuery(id+"F0.wireOp",EDGE,"E1")])]}),"instanceName":"1"}),"instanceName":"1"}),"instanceName":"1"}),"instanceName":"1"}),"instanceName":"1"}),"instanceName":"1"}),"instanceName":"1"}),"instanceName":"1"}),"instanceName":"1"});
            var Q765;
            Q765=makeQuery(id+"F11.opPattern","COPY",BODY,{"derivedFrom":makeQuery(id+"F10.opPattern","COPY",BODY,{"derivedFrom":makeQuery(id+"F9.opPattern","COPY",BODY,{"derivedFrom":makeQuery(id+"F8.opPattern","COPY",BODY,{"derivedFrom":makeQuery(id+"F7.opPattern","COPY",BODY,{"derivedFrom":makeQuery(id+"F6.opPattern","COPY",BODY,{"derivedFrom":makeQuery(id+"F5.opPattern","COPY",BODY,{"derivedFrom":makeQuery(id+"F4.opPattern","COPY",BODY,{"derivedFrom":makeQuery(id+"F1.opRevolve","SWEPT_BODY",BODY,{"disambiguationData":[OSD([sQuery(id+"F0.wireOp",EDGE,"E1")])]}),"instanceName":"1"}),"instanceName":"1"}),"instanceName":"1"}),"instanceName":"1"}),"instanceName":"1"}),"instanceName":"1"}),"instanceName":"1"}),"instanceName":"1"});
            var Q766;
            Q766=makeQuery(id+"F11.opPattern","COPY",BODY,{"derivedFrom":makeQuery(id+"F10.opPattern","COPY",BODY,{"derivedFrom":makeQuery(id+"F9.opPattern","COPY",BODY,{"derivedFrom":makeQuery(id+"F8.opPattern","COPY",BODY,{"derivedFrom":makeQuery(id+"F7.opPattern","COPY",BODY,{"derivedFrom":makeQuery(id+"F6.opPattern","COPY",BODY,{"derivedFrom":makeQuery(id+"F5.opPattern","COPY",BODY,{"derivedFrom":makeQuery(id+"F4.opPattern","COPY",BODY,{"derivedFrom":makeQuery(id+"F2.opPattern","COPY",BODY,{"derivedFrom":makeQuery(id+"F1.opRevolve","SWEPT_BODY",BODY,{"disambiguationData":[OSD([sQuery(id+"F0.wireOp",EDGE,"E1")])]}),"instanceName":"1"}),"instanceName":"1"}),"instanceName":"1"}),"instanceName":"1"}),"instanceName":"1"}),"instanceName":"1"}),"instanceName":"1"}),"instanceName":"1"}),"instanceName":"1"});
            var Q767;
            Q767=makeQuery(id+"F11.opPattern","COPY",BODY,{"derivedFrom":makeQuery(id+"F10.opPattern","COPY",BODY,{"derivedFrom":makeQuery(id+"F9.opPattern","COPY",BODY,{"derivedFrom":makeQuery(id+"F8.opPattern","COPY",BODY,{"derivedFrom":makeQuery(id+"F7.opPattern","COPY",BODY,{"derivedFrom":makeQuery(id+"F6.opPattern","COPY",BODY,{"derivedFrom":makeQuery(id+"F5.opPattern","COPY",BODY,{"derivedFrom":makeQuery(id+"F4.opPattern","COPY",BODY,{"derivedFrom":makeQuery(id+"F3.opPattern","COPY",BODY,{"derivedFrom":makeQuery(id+"F2.opPattern","COPY",BODY,{"derivedFrom":makeQuery(id+"F1.opRevolve","SWEPT_BODY",BODY,{"disambiguationData":[OSD([sQuery(id+"F0.wireOp",EDGE,"E1")])]}),"instanceName":"1"}),"instanceName":"1"}),"instanceName":"1"}),"instanceName":"1"}),"instanceName":"1"}),"instanceName":"1"}),"instanceName":"1"}),"instanceName":"1"}),"instanceName":"1"}),"instanceName":"1"});
            transform(context, id + "F12", {"entities" : qUnion([Q0, Q1, Q2, Q3, Q4, Q5, Q6, Q7, Q8, Q9, Q10, Q11, Q12, Q13, Q14, Q15, Q16, Q17, Q18, Q19, Q20, Q21, Q22, Q23, Q24, Q25, Q26, Q27, Q28, Q29, Q30, Q31, Q32, Q33, Q34, Q35, Q36, Q37, Q38, Q39, Q40, Q41, Q42, Q43, Q44, Q45, Q46, Q47, Q48, Q49, Q50, Q51, Q52, Q53, Q54, Q55, Q56, Q57, Q58, Q59, Q60, Q61, Q62, Q63, Q64, Q65, Q66, Q67, Q68, Q69, Q70, Q71, Q72, Q73, Q74, Q75, Q76, Q77, Q78, Q79, Q80, Q81, Q82, Q83, Q84, Q85, Q86, Q87, Q88, Q89, Q90, Q91, Q92, Q93, Q94, Q95, Q96, Q97, Q98, Q99, Q100, Q101, Q102, Q103, Q104, Q105, Q106, Q107, Q108, Q109, Q110, Q111, Q112, Q113, Q114, Q115, Q116, Q117, Q118, Q119, Q120, Q121, Q122, Q123, Q124, Q125, Q126, Q127, Q128, Q129, Q130, Q131, Q132, Q133, Q134, Q135, Q136, Q137, Q138, Q139, Q140, Q141, Q142, Q143, Q144, Q145, Q146, Q147, Q148, Q149, Q150, Q151, Q152, Q153, Q154, Q155, Q156, Q157, Q158, Q159, Q160, Q161, Q162, Q163, Q164, Q165, Q166, Q167, Q168, Q169, Q170, Q171, Q172, Q173, Q174, Q175, Q176, Q177, Q178, Q179, Q180, Q181, Q182, Q183, Q184, Q185, Q186, Q187, Q188, Q189, Q190, Q191, Q192, Q193, Q194, Q195, Q196, Q197, Q198, Q199, Q200, Q201, Q202, Q203, Q204, Q205, Q206, Q207, Q208, Q209, Q210, Q211, Q212, Q213, Q214, Q215, Q216, Q217, Q218, Q219, Q220, Q221, Q222, Q223, Q224, Q225, Q226, Q227, Q228, Q229, Q230, Q231, Q232, Q233, Q234, Q235, Q236, Q237, Q238, Q239, Q240, Q241, Q242, Q243, Q244, Q245, Q246, Q247, Q248, Q249, Q250, Q251, Q252, Q253, Q254, Q255, Q256, Q257, Q258, Q259, Q260, Q261, Q262, Q263, Q264, Q265, Q266, Q267, Q268, Q269, Q270, Q271, Q272, Q273, Q274, Q275, Q276, Q277, Q278, Q279, Q280, Q281, Q282, Q283, Q284, Q285, Q286, Q287, Q288, Q289, Q290, Q291, Q292, Q293, Q294, Q295, Q296, Q297, Q298, Q299, Q300, Q301, Q302, Q303, Q304, Q305, Q306, Q307, Q308, Q309, Q310, Q311, Q312, Q313, Q314, Q315, Q316, Q317, Q318, Q319, Q320, Q321, Q322, Q323, Q324, Q325, Q326, Q327, Q328, Q329, Q330, Q331, Q332, Q333, Q334, Q335, Q336, Q337, Q338, Q339, Q340, Q341, Q342, Q343, Q344, Q345, Q346, Q347, Q348, Q349, Q350, Q351, Q352, Q353, Q354, Q355, Q356, Q357, Q358, Q359, Q360, Q361, Q362, Q363, Q364, Q365, Q366, Q367, Q368, Q369, Q370, Q371, Q372, Q373, Q374, Q375, Q376, Q377, Q378, Q379, Q380, Q381, Q382, Q383, Q384, Q385, Q386, Q387, Q388, Q389, Q390, Q391, Q392, Q393, Q394, Q395, Q396, Q397, Q398, Q399, Q400, Q401, Q402, Q403, Q404, Q405, Q406, Q407, Q408, Q409, Q410, Q411, Q412, Q413, Q414, Q415, Q416, Q417, Q418, Q419, Q420, Q421, Q422, Q423, Q424, Q425, Q426, Q427, Q428, Q429, Q430, Q431, Q432, Q433, Q434, Q435, Q436, Q437, Q438, Q439, Q440, Q441, Q442, Q443, Q444, Q445, Q446, Q447, Q448, Q449, Q450, Q451, Q452, Q453, Q454, Q455, Q456, Q457, Q458, Q459, Q460, Q461, Q462, Q463, Q464, Q465, Q466, Q467, Q468, Q469, Q470, Q471, Q472, Q473, Q474, Q475, Q476, Q477, Q478, Q479, Q480, Q481, Q482, Q483, Q484, Q485, Q486, Q487, Q488, Q489, Q490, Q491, Q492, Q493, Q494, Q495, Q496, Q497, Q498, Q499, Q500, Q501, Q502, Q503, Q504, Q505, Q506, Q507, Q508, Q509, Q510, Q511, Q512, Q513, Q514, Q515, Q516, Q517, Q518, Q519, Q520, Q521, Q522, Q523, Q524, Q525, Q526, Q527, Q528, Q529, Q530, Q531, Q532, Q533, Q534, Q535, Q536, Q537, Q538, Q539, Q540, Q541, Q542, Q543, Q544, Q545, Q546, Q547, Q548, Q549, Q550, Q551, Q552, Q553, Q554, Q555, Q556, Q557, Q558, Q559, Q560, Q561, Q562, Q563, Q564, Q565, Q566, Q567, Q568, Q569, Q570, Q571, Q572, Q573, Q574, Q575, Q576, Q577, Q578, Q579, Q580, Q581, Q582, Q583, Q584, Q585, Q586, Q587, Q588, Q589, Q590, Q591, Q592, Q593, Q594, Q595, Q596, Q597, Q598, Q599, Q600, Q601, Q602, Q603, Q604, Q605, Q606, Q607, Q608, Q609, Q610, Q611, Q612, Q613, Q614, Q615, Q616, Q617, Q618, Q619, Q620, Q621, Q622, Q623, Q624, Q625, Q626, Q627, Q628, Q629, Q630, Q631, Q632, Q633, Q634, Q635, Q636, Q637, Q638, Q639, Q640, Q641, Q642, Q643, Q644, Q645, Q646, Q647, Q648, Q649, Q650, Q651, Q652, Q653, Q654, Q655, Q656, Q657, Q658, Q659, Q660, Q661, Q662, Q663, Q664, Q665, Q666, Q667, Q668, Q669, Q670, Q671, Q672, Q673, Q674, Q675, Q676, Q677, Q678, Q679, Q680, Q681, Q682, Q683, Q684, Q685, Q686, Q687, Q688, Q689, Q690, Q691, Q692, Q693, Q694, Q695, Q696, Q697, Q698, Q699, Q700, Q701, Q702, Q703, Q704, Q705, Q706, Q707, Q708, Q709, Q710, Q711, Q712, Q713, Q714, Q715, Q716, Q717, Q718, Q719, Q720, Q721, Q722, Q723, Q724, Q725, Q726, Q727, Q728, Q729, Q730, Q731, Q732, Q733, Q734, Q735, Q736, Q737, Q738, Q739, Q740, Q741, Q742, Q743, Q744, Q745, Q746, Q747, Q748, Q749, Q750, Q751, Q752, Q753, Q754, Q755, Q756, Q757, Q758, Q759, Q760, Q761, Q762, Q763, Q764, Q765, Q766, Q767]), "transformType" : TransformType.TRANSLATION_3D, "dx" : 0 * mm, "dy" : 0.56 * mm, "dz" : 0 * mm, "makeCopy" : true});
        }
        {
            var Q0;
            Q0=makeQuery(id+"F1.opRevolve","SWEPT_BODY",BODY,{"disambiguationData":[OSD([sQuery(id+"F0.wireOp",EDGE,"E1")])]});
            var Q1;
            Q1=makeQuery(id+"F2.opPattern","COPY",BODY,{"derivedFrom":makeQuery(id+"F1.opRevolve","SWEPT_BODY",BODY,{"disambiguationData":[OSD([sQuery(id+"F0.wireOp",EDGE,"E1")])]}),"instanceName":"1"});
            var Q2;
            Q2=makeQuery(id+"F3.opPattern","COPY",BODY,{"derivedFrom":makeQuery(id+"F2.opPattern","COPY",BODY,{"derivedFrom":makeQuery(id+"F1.opRevolve","SWEPT_BODY",BODY,{"disambiguationData":[OSD([sQuery(id+"F0.wireOp",EDGE,"E1")])]}),"instanceName":"1"}),"instanceName":"1"});
            var Q3;
            Q3=makeQuery(id+"F4.opPattern","COPY",BODY,{"derivedFrom":makeQuery(id+"F1.opRevolve","SWEPT_BODY",BODY,{"disambiguationData":[OSD([sQuery(id+"F0.wireOp",EDGE,"E1")])]}),"instanceName":"1"});
            var Q4;
            Q4=makeQuery(id+"F4.opPattern","COPY",BODY,{"derivedFrom":makeQuery(id+"F2.opPattern","COPY",BODY,{"derivedFrom":makeQuery(id+"F1.opRevolve","SWEPT_BODY",BODY,{"disambiguationData":[OSD([sQuery(id+"F0.wireOp",EDGE,"E1")])]}),"instanceName":"1"}),"instanceName":"1"});
            var Q5;
            Q5=makeQuery(id+"F4.opPattern","COPY",BODY,{"derivedFrom":makeQuery(id+"F3.opPattern","COPY",BODY,{"derivedFrom":makeQuery(id+"F2.opPattern","COPY",BODY,{"derivedFrom":makeQuery(id+"F1.opRevolve","SWEPT_BODY",BODY,{"disambiguationData":[OSD([sQuery(id+"F0.wireOp",EDGE,"E1")])]}),"instanceName":"1"}),"instanceName":"1"}),"instanceName":"1"});
            var Q6;
            Q6=makeQuery(id+"F5.opPattern","COPY",BODY,{"derivedFrom":makeQuery(id+"F1.opRevolve","SWEPT_BODY",BODY,{"disambiguationData":[OSD([sQuery(id+"F0.wireOp",EDGE,"E1")])]}),"instanceName":"1"});
            var Q7;
            Q7=makeQuery(id+"F5.opPattern","COPY",BODY,{"derivedFrom":makeQuery(id+"F2.opPattern","COPY",BODY,{"derivedFrom":makeQuery(id+"F1.opRevolve","SWEPT_BODY",BODY,{"disambiguationData":[OSD([sQuery(id+"F0.wireOp",EDGE,"E1")])]}),"instanceName":"1"}),"instanceName":"1"});
            var Q8;
            Q8=makeQuery(id+"F5.opPattern","COPY",BODY,{"derivedFrom":makeQuery(id+"F3.opPattern","COPY",BODY,{"derivedFrom":makeQuery(id+"F2.opPattern","COPY",BODY,{"derivedFrom":makeQuery(id+"F1.opRevolve","SWEPT_BODY",BODY,{"disambiguationData":[OSD([sQuery(id+"F0.wireOp",EDGE,"E1")])]}),"instanceName":"1"}),"instanceName":"1"}),"instanceName":"1"});
            var Q9;
            Q9=makeQuery(id+"F5.opPattern","COPY",BODY,{"derivedFrom":makeQuery(id+"F4.opPattern","COPY",BODY,{"derivedFrom":makeQuery(id+"F1.opRevolve","SWEPT_BODY",BODY,{"disambiguationData":[OSD([sQuery(id+"F0.wireOp",EDGE,"E1")])]}),"instanceName":"1"}),"instanceName":"1"});
            var Q10;
            Q10=makeQuery(id+"F5.opPattern","COPY",BODY,{"derivedFrom":makeQuery(id+"F4.opPattern","COPY",BODY,{"derivedFrom":makeQuery(id+"F2.opPattern","COPY",BODY,{"derivedFrom":makeQuery(id+"F1.opRevolve","SWEPT_BODY",BODY,{"disambiguationData":[OSD([sQuery(id+"F0.wireOp",EDGE,"E1")])]}),"instanceName":"1"}),"instanceName":"1"}),"instanceName":"1"});
            var Q11;
            Q11=makeQuery(id+"F5.opPattern","COPY",BODY,{"derivedFrom":makeQuery(id+"F4.opPattern","COPY",BODY,{"derivedFrom":makeQuery(id+"F3.opPattern","COPY",BODY,{"derivedFrom":makeQuery(id+"F2.opPattern","COPY",BODY,{"derivedFrom":makeQuery(id+"F1.opRevolve","SWEPT_BODY",BODY,{"disambiguationData":[OSD([sQuery(id+"F0.wireOp",EDGE,"E1")])]}),"instanceName":"1"}),"instanceName":"1"}),"instanceName":"1"}),"instanceName":"1"});
            var Q12;
            Q12=makeQuery(id+"F6.opPattern","COPY",BODY,{"derivedFrom":makeQuery(id+"F1.opRevolve","SWEPT_BODY",BODY,{"disambiguationData":[OSD([sQuery(id+"F0.wireOp",EDGE,"E1")])]}),"instanceName":"1"});
            var Q13;
            Q13=makeQuery(id+"F6.opPattern","COPY",BODY,{"derivedFrom":makeQuery(id+"F2.opPattern","COPY",BODY,{"derivedFrom":makeQuery(id+"F1.opRevolve","SWEPT_BODY",BODY,{"disambiguationData":[OSD([sQuery(id+"F0.wireOp",EDGE,"E1")])]}),"instanceName":"1"}),"instanceName":"1"});
            var Q14;
            Q14=makeQuery(id+"F6.opPattern","COPY",BODY,{"derivedFrom":makeQuery(id+"F3.opPattern","COPY",BODY,{"derivedFrom":makeQuery(id+"F2.opPattern","COPY",BODY,{"derivedFrom":makeQuery(id+"F1.opRevolve","SWEPT_BODY",BODY,{"disambiguationData":[OSD([sQuery(id+"F0.wireOp",EDGE,"E1")])]}),"instanceName":"1"}),"instanceName":"1"}),"instanceName":"1"});
            var Q15;
            Q15=makeQuery(id+"F6.opPattern","COPY",BODY,{"derivedFrom":makeQuery(id+"F4.opPattern","COPY",BODY,{"derivedFrom":makeQuery(id+"F1.opRevolve","SWEPT_BODY",BODY,{"disambiguationData":[OSD([sQuery(id+"F0.wireOp",EDGE,"E1")])]}),"instanceName":"1"}),"instanceName":"1"});
            var Q16;
            Q16=makeQuery(id+"F6.opPattern","COPY",BODY,{"derivedFrom":makeQuery(id+"F4.opPattern","COPY",BODY,{"derivedFrom":makeQuery(id+"F2.opPattern","COPY",BODY,{"derivedFrom":makeQuery(id+"F1.opRevolve","SWEPT_BODY",BODY,{"disambiguationData":[OSD([sQuery(id+"F0.wireOp",EDGE,"E1")])]}),"instanceName":"1"}),"instanceName":"1"}),"instanceName":"1"});
            var Q17;
            Q17=makeQuery(id+"F6.opPattern","COPY",BODY,{"derivedFrom":makeQuery(id+"F4.opPattern","COPY",BODY,{"derivedFrom":makeQuery(id+"F3.opPattern","COPY",BODY,{"derivedFrom":makeQuery(id+"F2.opPattern","COPY",BODY,{"derivedFrom":makeQuery(id+"F1.opRevolve","SWEPT_BODY",BODY,{"disambiguationData":[OSD([sQuery(id+"F0.wireOp",EDGE,"E1")])]}),"instanceName":"1"}),"instanceName":"1"}),"instanceName":"1"}),"instanceName":"1"});
            var Q18;
            Q18=makeQuery(id+"F6.opPattern","COPY",BODY,{"derivedFrom":makeQuery(id+"F5.opPattern","COPY",BODY,{"derivedFrom":makeQuery(id+"F1.opRevolve","SWEPT_BODY",BODY,{"disambiguationData":[OSD([sQuery(id+"F0.wireOp",EDGE,"E1")])]}),"instanceName":"1"}),"instanceName":"1"});
            var Q19;
            Q19=makeQuery(id+"F6.opPattern","COPY",BODY,{"derivedFrom":makeQuery(id+"F5.opPattern","COPY",BODY,{"derivedFrom":makeQuery(id+"F2.opPattern","COPY",BODY,{"derivedFrom":makeQuery(id+"F1.opRevolve","SWEPT_BODY",BODY,{"disambiguationData":[OSD([sQuery(id+"F0.wireOp",EDGE,"E1")])]}),"instanceName":"1"}),"instanceName":"1"}),"instanceName":"1"});
            var Q20;
            Q20=makeQuery(id+"F6.opPattern","COPY",BODY,{"derivedFrom":makeQuery(id+"F5.opPattern","COPY",BODY,{"derivedFrom":makeQuery(id+"F3.opPattern","COPY",BODY,{"derivedFrom":makeQuery(id+"F2.opPattern","COPY",BODY,{"derivedFrom":makeQuery(id+"F1.opRevolve","SWEPT_BODY",BODY,{"disambiguationData":[OSD([sQuery(id+"F0.wireOp",EDGE,"E1")])]}),"instanceName":"1"}),"instanceName":"1"}),"instanceName":"1"}),"instanceName":"1"});
            var Q21;
            Q21=makeQuery(id+"F6.opPattern","COPY",BODY,{"derivedFrom":makeQuery(id+"F5.opPattern","COPY",BODY,{"derivedFrom":makeQuery(id+"F4.opPattern","COPY",BODY,{"derivedFrom":makeQuery(id+"F1.opRevolve","SWEPT_BODY",BODY,{"disambiguationData":[OSD([sQuery(id+"F0.wireOp",EDGE,"E1")])]}),"instanceName":"1"}),"instanceName":"1"}),"instanceName":"1"});
            var Q22;
            Q22=makeQuery(id+"F6.opPattern","COPY",BODY,{"derivedFrom":makeQuery(id+"F5.opPattern","COPY",BODY,{"derivedFrom":makeQuery(id+"F4.opPattern","COPY",BODY,{"derivedFrom":makeQuery(id+"F2.opPattern","COPY",BODY,{"derivedFrom":makeQuery(id+"F1.opRevolve","SWEPT_BODY",BODY,{"disambiguationData":[OSD([sQuery(id+"F0.wireOp",EDGE,"E1")])]}),"instanceName":"1"}),"instanceName":"1"}),"instanceName":"1"}),"instanceName":"1"});
            var Q23;
            Q23=makeQuery(id+"F6.opPattern","COPY",BODY,{"derivedFrom":makeQuery(id+"F5.opPattern","COPY",BODY,{"derivedFrom":makeQuery(id+"F4.opPattern","COPY",BODY,{"derivedFrom":makeQuery(id+"F3.opPattern","COPY",BODY,{"derivedFrom":makeQuery(id+"F2.opPattern","COPY",BODY,{"derivedFrom":makeQuery(id+"F1.opRevolve","SWEPT_BODY",BODY,{"disambiguationData":[OSD([sQuery(id+"F0.wireOp",EDGE,"E1")])]}),"instanceName":"1"}),"instanceName":"1"}),"instanceName":"1"}),"instanceName":"1"}),"instanceName":"1"});
            var Q24;
            Q24=makeQuery(id+"F7.opPattern","COPY",BODY,{"derivedFrom":makeQuery(id+"F1.opRevolve","SWEPT_BODY",BODY,{"disambiguationData":[OSD([sQuery(id+"F0.wireOp",EDGE,"E1")])]}),"instanceName":"1"});
            var Q25;
            Q25=makeQuery(id+"F7.opPattern","COPY",BODY,{"derivedFrom":makeQuery(id+"F2.opPattern","COPY",BODY,{"derivedFrom":makeQuery(id+"F1.opRevolve","SWEPT_BODY",BODY,{"disambiguationData":[OSD([sQuery(id+"F0.wireOp",EDGE,"E1")])]}),"instanceName":"1"}),"instanceName":"1"});
            var Q26;
            Q26=makeQuery(id+"F7.opPattern","COPY",BODY,{"derivedFrom":makeQuery(id+"F3.opPattern","COPY",BODY,{"derivedFrom":makeQuery(id+"F2.opPattern","COPY",BODY,{"derivedFrom":makeQuery(id+"F1.opRevolve","SWEPT_BODY",BODY,{"disambiguationData":[OSD([sQuery(id+"F0.wireOp",EDGE,"E1")])]}),"instanceName":"1"}),"instanceName":"1"}),"instanceName":"1"});
            var Q27;
            Q27=makeQuery(id+"F7.opPattern","COPY",BODY,{"derivedFrom":makeQuery(id+"F4.opPattern","COPY",BODY,{"derivedFrom":makeQuery(id+"F1.opRevolve","SWEPT_BODY",BODY,{"disambiguationData":[OSD([sQuery(id+"F0.wireOp",EDGE,"E1")])]}),"instanceName":"1"}),"instanceName":"1"});
            var Q28;
            Q28=makeQuery(id+"F7.opPattern","COPY",BODY,{"derivedFrom":makeQuery(id+"F4.opPattern","COPY",BODY,{"derivedFrom":makeQuery(id+"F2.opPattern","COPY",BODY,{"derivedFrom":makeQuery(id+"F1.opRevolve","SWEPT_BODY",BODY,{"disambiguationData":[OSD([sQuery(id+"F0.wireOp",EDGE,"E1")])]}),"instanceName":"1"}),"instanceName":"1"}),"instanceName":"1"});
            var Q29;
            Q29=makeQuery(id+"F7.opPattern","COPY",BODY,{"derivedFrom":makeQuery(id+"F4.opPattern","COPY",BODY,{"derivedFrom":makeQuery(id+"F3.opPattern","COPY",BODY,{"derivedFrom":makeQuery(id+"F2.opPattern","COPY",BODY,{"derivedFrom":makeQuery(id+"F1.opRevolve","SWEPT_BODY",BODY,{"disambiguationData":[OSD([sQuery(id+"F0.wireOp",EDGE,"E1")])]}),"instanceName":"1"}),"instanceName":"1"}),"instanceName":"1"}),"instanceName":"1"});
            var Q30;
            Q30=makeQuery(id+"F7.opPattern","COPY",BODY,{"derivedFrom":makeQuery(id+"F5.opPattern","COPY",BODY,{"derivedFrom":makeQuery(id+"F1.opRevolve","SWEPT_BODY",BODY,{"disambiguationData":[OSD([sQuery(id+"F0.wireOp",EDGE,"E1")])]}),"instanceName":"1"}),"instanceName":"1"});
            var Q31;
            Q31=makeQuery(id+"F7.opPattern","COPY",BODY,{"derivedFrom":makeQuery(id+"F5.opPattern","COPY",BODY,{"derivedFrom":makeQuery(id+"F2.opPattern","COPY",BODY,{"derivedFrom":makeQuery(id+"F1.opRevolve","SWEPT_BODY",BODY,{"disambiguationData":[OSD([sQuery(id+"F0.wireOp",EDGE,"E1")])]}),"instanceName":"1"}),"instanceName":"1"}),"instanceName":"1"});
            var Q32;
            Q32=makeQuery(id+"F7.opPattern","COPY",BODY,{"derivedFrom":makeQuery(id+"F5.opPattern","COPY",BODY,{"derivedFrom":makeQuery(id+"F3.opPattern","COPY",BODY,{"derivedFrom":makeQuery(id+"F2.opPattern","COPY",BODY,{"derivedFrom":makeQuery(id+"F1.opRevolve","SWEPT_BODY",BODY,{"disambiguationData":[OSD([sQuery(id+"F0.wireOp",EDGE,"E1")])]}),"instanceName":"1"}),"instanceName":"1"}),"instanceName":"1"}),"instanceName":"1"});
            var Q33;
            Q33=makeQuery(id+"F7.opPattern","COPY",BODY,{"derivedFrom":makeQuery(id+"F5.opPattern","COPY",BODY,{"derivedFrom":makeQuery(id+"F4.opPattern","COPY",BODY,{"derivedFrom":makeQuery(id+"F1.opRevolve","SWEPT_BODY",BODY,{"disambiguationData":[OSD([sQuery(id+"F0.wireOp",EDGE,"E1")])]}),"instanceName":"1"}),"instanceName":"1"}),"instanceName":"1"});
            var Q34;
            Q34=makeQuery(id+"F7.opPattern","COPY",BODY,{"derivedFrom":makeQuery(id+"F5.opPattern","COPY",BODY,{"derivedFrom":makeQuery(id+"F4.opPattern","COPY",BODY,{"derivedFrom":makeQuery(id+"F2.opPattern","COPY",BODY,{"derivedFrom":makeQuery(id+"F1.opRevolve","SWEPT_BODY",BODY,{"disambiguationData":[OSD([sQuery(id+"F0.wireOp",EDGE,"E1")])]}),"instanceName":"1"}),"instanceName":"1"}),"instanceName":"1"}),"instanceName":"1"});
            var Q35;
            Q35=makeQuery(id+"F7.opPattern","COPY",BODY,{"derivedFrom":makeQuery(id+"F5.opPattern","COPY",BODY,{"derivedFrom":makeQuery(id+"F4.opPattern","COPY",BODY,{"derivedFrom":makeQuery(id+"F3.opPattern","COPY",BODY,{"derivedFrom":makeQuery(id+"F2.opPattern","COPY",BODY,{"derivedFrom":makeQuery(id+"F1.opRevolve","SWEPT_BODY",BODY,{"disambiguationData":[OSD([sQuery(id+"F0.wireOp",EDGE,"E1")])]}),"instanceName":"1"}),"instanceName":"1"}),"instanceName":"1"}),"instanceName":"1"}),"instanceName":"1"});
            var Q36;
            Q36=makeQuery(id+"F7.opPattern","COPY",BODY,{"derivedFrom":makeQuery(id+"F6.opPattern","COPY",BODY,{"derivedFrom":makeQuery(id+"F1.opRevolve","SWEPT_BODY",BODY,{"disambiguationData":[OSD([sQuery(id+"F0.wireOp",EDGE,"E1")])]}),"instanceName":"1"}),"instanceName":"1"});
            var Q37;
            Q37=makeQuery(id+"F7.opPattern","COPY",BODY,{"derivedFrom":makeQuery(id+"F6.opPattern","COPY",BODY,{"derivedFrom":makeQuery(id+"F2.opPattern","COPY",BODY,{"derivedFrom":makeQuery(id+"F1.opRevolve","SWEPT_BODY",BODY,{"disambiguationData":[OSD([sQuery(id+"F0.wireOp",EDGE,"E1")])]}),"instanceName":"1"}),"instanceName":"1"}),"instanceName":"1"});
            var Q38;
            Q38=makeQuery(id+"F7.opPattern","COPY",BODY,{"derivedFrom":makeQuery(id+"F6.opPattern","COPY",BODY,{"derivedFrom":makeQuery(id+"F3.opPattern","COPY",BODY,{"derivedFrom":makeQuery(id+"F2.opPattern","COPY",BODY,{"derivedFrom":makeQuery(id+"F1.opRevolve","SWEPT_BODY",BODY,{"disambiguationData":[OSD([sQuery(id+"F0.wireOp",EDGE,"E1")])]}),"instanceName":"1"}),"instanceName":"1"}),"instanceName":"1"}),"instanceName":"1"});
            var Q39;
            Q39=makeQuery(id+"F7.opPattern","COPY",BODY,{"derivedFrom":makeQuery(id+"F6.opPattern","COPY",BODY,{"derivedFrom":makeQuery(id+"F4.opPattern","COPY",BODY,{"derivedFrom":makeQuery(id+"F1.opRevolve","SWEPT_BODY",BODY,{"disambiguationData":[OSD([sQuery(id+"F0.wireOp",EDGE,"E1")])]}),"instanceName":"1"}),"instanceName":"1"}),"instanceName":"1"});
            var Q40;
            Q40=makeQuery(id+"F7.opPattern","COPY",BODY,{"derivedFrom":makeQuery(id+"F6.opPattern","COPY",BODY,{"derivedFrom":makeQuery(id+"F4.opPattern","COPY",BODY,{"derivedFrom":makeQuery(id+"F2.opPattern","COPY",BODY,{"derivedFrom":makeQuery(id+"F1.opRevolve","SWEPT_BODY",BODY,{"disambiguationData":[OSD([sQuery(id+"F0.wireOp",EDGE,"E1")])]}),"instanceName":"1"}),"instanceName":"1"}),"instanceName":"1"}),"instanceName":"1"});
            var Q41;
            Q41=makeQuery(id+"F7.opPattern","COPY",BODY,{"derivedFrom":makeQuery(id+"F6.opPattern","COPY",BODY,{"derivedFrom":makeQuery(id+"F4.opPattern","COPY",BODY,{"derivedFrom":makeQuery(id+"F3.opPattern","COPY",BODY,{"derivedFrom":makeQuery(id+"F2.opPattern","COPY",BODY,{"derivedFrom":makeQuery(id+"F1.opRevolve","SWEPT_BODY",BODY,{"disambiguationData":[OSD([sQuery(id+"F0.wireOp",EDGE,"E1")])]}),"instanceName":"1"}),"instanceName":"1"}),"instanceName":"1"}),"instanceName":"1"}),"instanceName":"1"});
            var Q42;
            Q42=makeQuery(id+"F7.opPattern","COPY",BODY,{"derivedFrom":makeQuery(id+"F6.opPattern","COPY",BODY,{"derivedFrom":makeQuery(id+"F5.opPattern","COPY",BODY,{"derivedFrom":makeQuery(id+"F1.opRevolve","SWEPT_BODY",BODY,{"disambiguationData":[OSD([sQuery(id+"F0.wireOp",EDGE,"E1")])]}),"instanceName":"1"}),"instanceName":"1"}),"instanceName":"1"});
            var Q43;
            Q43=makeQuery(id+"F7.opPattern","COPY",BODY,{"derivedFrom":makeQuery(id+"F6.opPattern","COPY",BODY,{"derivedFrom":makeQuery(id+"F5.opPattern","COPY",BODY,{"derivedFrom":makeQuery(id+"F2.opPattern","COPY",BODY,{"derivedFrom":makeQuery(id+"F1.opRevolve","SWEPT_BODY",BODY,{"disambiguationData":[OSD([sQuery(id+"F0.wireOp",EDGE,"E1")])]}),"instanceName":"1"}),"instanceName":"1"}),"instanceName":"1"}),"instanceName":"1"});
            var Q44;
            Q44=makeQuery(id+"F7.opPattern","COPY",BODY,{"derivedFrom":makeQuery(id+"F6.opPattern","COPY",BODY,{"derivedFrom":makeQuery(id+"F5.opPattern","COPY",BODY,{"derivedFrom":makeQuery(id+"F3.opPattern","COPY",BODY,{"derivedFrom":makeQuery(id+"F2.opPattern","COPY",BODY,{"derivedFrom":makeQuery(id+"F1.opRevolve","SWEPT_BODY",BODY,{"disambiguationData":[OSD([sQuery(id+"F0.wireOp",EDGE,"E1")])]}),"instanceName":"1"}),"instanceName":"1"}),"instanceName":"1"}),"instanceName":"1"}),"instanceName":"1"});
            var Q45;
            Q45=makeQuery(id+"F7.opPattern","COPY",BODY,{"derivedFrom":makeQuery(id+"F6.opPattern","COPY",BODY,{"derivedFrom":makeQuery(id+"F5.opPattern","COPY",BODY,{"derivedFrom":makeQuery(id+"F4.opPattern","COPY",BODY,{"derivedFrom":makeQuery(id+"F1.opRevolve","SWEPT_BODY",BODY,{"disambiguationData":[OSD([sQuery(id+"F0.wireOp",EDGE,"E1")])]}),"instanceName":"1"}),"instanceName":"1"}),"instanceName":"1"}),"instanceName":"1"});
            var Q46;
            Q46=makeQuery(id+"F7.opPattern","COPY",BODY,{"derivedFrom":makeQuery(id+"F6.opPattern","COPY",BODY,{"derivedFrom":makeQuery(id+"F5.opPattern","COPY",BODY,{"derivedFrom":makeQuery(id+"F4.opPattern","COPY",BODY,{"derivedFrom":makeQuery(id+"F2.opPattern","COPY",BODY,{"derivedFrom":makeQuery(id+"F1.opRevolve","SWEPT_BODY",BODY,{"disambiguationData":[OSD([sQuery(id+"F0.wireOp",EDGE,"E1")])]}),"instanceName":"1"}),"instanceName":"1"}),"instanceName":"1"}),"instanceName":"1"}),"instanceName":"1"});
            var Q47;
            Q47=makeQuery(id+"F7.opPattern","COPY",BODY,{"derivedFrom":makeQuery(id+"F6.opPattern","COPY",BODY,{"derivedFrom":makeQuery(id+"F5.opPattern","COPY",BODY,{"derivedFrom":makeQuery(id+"F4.opPattern","COPY",BODY,{"derivedFrom":makeQuery(id+"F3.opPattern","COPY",BODY,{"derivedFrom":makeQuery(id+"F2.opPattern","COPY",BODY,{"derivedFrom":makeQuery(id+"F1.opRevolve","SWEPT_BODY",BODY,{"disambiguationData":[OSD([sQuery(id+"F0.wireOp",EDGE,"E1")])]}),"instanceName":"1"}),"instanceName":"1"}),"instanceName":"1"}),"instanceName":"1"}),"instanceName":"1"}),"instanceName":"1"});
            var Q48;
            Q48=makeQuery(id+"F8.opPattern","COPY",BODY,{"derivedFrom":makeQuery(id+"F1.opRevolve","SWEPT_BODY",BODY,{"disambiguationData":[OSD([sQuery(id+"F0.wireOp",EDGE,"E1")])]}),"instanceName":"1"});
            var Q49;
            Q49=makeQuery(id+"F8.opPattern","COPY",BODY,{"derivedFrom":makeQuery(id+"F2.opPattern","COPY",BODY,{"derivedFrom":makeQuery(id+"F1.opRevolve","SWEPT_BODY",BODY,{"disambiguationData":[OSD([sQuery(id+"F0.wireOp",EDGE,"E1")])]}),"instanceName":"1"}),"instanceName":"1"});
            var Q50;
            Q50=makeQuery(id+"F8.opPattern","COPY",BODY,{"derivedFrom":makeQuery(id+"F3.opPattern","COPY",BODY,{"derivedFrom":makeQuery(id+"F2.opPattern","COPY",BODY,{"derivedFrom":makeQuery(id+"F1.opRevolve","SWEPT_BODY",BODY,{"disambiguationData":[OSD([sQuery(id+"F0.wireOp",EDGE,"E1")])]}),"instanceName":"1"}),"instanceName":"1"}),"instanceName":"1"});
            var Q51;
            Q51=makeQuery(id+"F8.opPattern","COPY",BODY,{"derivedFrom":makeQuery(id+"F4.opPattern","COPY",BODY,{"derivedFrom":makeQuery(id+"F1.opRevolve","SWEPT_BODY",BODY,{"disambiguationData":[OSD([sQuery(id+"F0.wireOp",EDGE,"E1")])]}),"instanceName":"1"}),"instanceName":"1"});
            var Q52;
            Q52=makeQuery(id+"F8.opPattern","COPY",BODY,{"derivedFrom":makeQuery(id+"F4.opPattern","COPY",BODY,{"derivedFrom":makeQuery(id+"F2.opPattern","COPY",BODY,{"derivedFrom":makeQuery(id+"F1.opRevolve","SWEPT_BODY",BODY,{"disambiguationData":[OSD([sQuery(id+"F0.wireOp",EDGE,"E1")])]}),"instanceName":"1"}),"instanceName":"1"}),"instanceName":"1"});
            var Q53;
            Q53=makeQuery(id+"F8.opPattern","COPY",BODY,{"derivedFrom":makeQuery(id+"F4.opPattern","COPY",BODY,{"derivedFrom":makeQuery(id+"F3.opPattern","COPY",BODY,{"derivedFrom":makeQuery(id+"F2.opPattern","COPY",BODY,{"derivedFrom":makeQuery(id+"F1.opRevolve","SWEPT_BODY",BODY,{"disambiguationData":[OSD([sQuery(id+"F0.wireOp",EDGE,"E1")])]}),"instanceName":"1"}),"instanceName":"1"}),"instanceName":"1"}),"instanceName":"1"});
            var Q54;
            Q54=makeQuery(id+"F8.opPattern","COPY",BODY,{"derivedFrom":makeQuery(id+"F5.opPattern","COPY",BODY,{"derivedFrom":makeQuery(id+"F1.opRevolve","SWEPT_BODY",BODY,{"disambiguationData":[OSD([sQuery(id+"F0.wireOp",EDGE,"E1")])]}),"instanceName":"1"}),"instanceName":"1"});
            var Q55;
            Q55=makeQuery(id+"F8.opPattern","COPY",BODY,{"derivedFrom":makeQuery(id+"F5.opPattern","COPY",BODY,{"derivedFrom":makeQuery(id+"F2.opPattern","COPY",BODY,{"derivedFrom":makeQuery(id+"F1.opRevolve","SWEPT_BODY",BODY,{"disambiguationData":[OSD([sQuery(id+"F0.wireOp",EDGE,"E1")])]}),"instanceName":"1"}),"instanceName":"1"}),"instanceName":"1"});
            var Q56;
            Q56=makeQuery(id+"F8.opPattern","COPY",BODY,{"derivedFrom":makeQuery(id+"F5.opPattern","COPY",BODY,{"derivedFrom":makeQuery(id+"F3.opPattern","COPY",BODY,{"derivedFrom":makeQuery(id+"F2.opPattern","COPY",BODY,{"derivedFrom":makeQuery(id+"F1.opRevolve","SWEPT_BODY",BODY,{"disambiguationData":[OSD([sQuery(id+"F0.wireOp",EDGE,"E1")])]}),"instanceName":"1"}),"instanceName":"1"}),"instanceName":"1"}),"instanceName":"1"});
            var Q57;
            Q57=makeQuery(id+"F8.opPattern","COPY",BODY,{"derivedFrom":makeQuery(id+"F5.opPattern","COPY",BODY,{"derivedFrom":makeQuery(id+"F4.opPattern","COPY",BODY,{"derivedFrom":makeQuery(id+"F1.opRevolve","SWEPT_BODY",BODY,{"disambiguationData":[OSD([sQuery(id+"F0.wireOp",EDGE,"E1")])]}),"instanceName":"1"}),"instanceName":"1"}),"instanceName":"1"});
            var Q58;
            Q58=makeQuery(id+"F8.opPattern","COPY",BODY,{"derivedFrom":makeQuery(id+"F5.opPattern","COPY",BODY,{"derivedFrom":makeQuery(id+"F4.opPattern","COPY",BODY,{"derivedFrom":makeQuery(id+"F2.opPattern","COPY",BODY,{"derivedFrom":makeQuery(id+"F1.opRevolve","SWEPT_BODY",BODY,{"disambiguationData":[OSD([sQuery(id+"F0.wireOp",EDGE,"E1")])]}),"instanceName":"1"}),"instanceName":"1"}),"instanceName":"1"}),"instanceName":"1"});
            var Q59;
            Q59=makeQuery(id+"F8.opPattern","COPY",BODY,{"derivedFrom":makeQuery(id+"F5.opPattern","COPY",BODY,{"derivedFrom":makeQuery(id+"F4.opPattern","COPY",BODY,{"derivedFrom":makeQuery(id+"F3.opPattern","COPY",BODY,{"derivedFrom":makeQuery(id+"F2.opPattern","COPY",BODY,{"derivedFrom":makeQuery(id+"F1.opRevolve","SWEPT_BODY",BODY,{"disambiguationData":[OSD([sQuery(id+"F0.wireOp",EDGE,"E1")])]}),"instanceName":"1"}),"instanceName":"1"}),"instanceName":"1"}),"instanceName":"1"}),"instanceName":"1"});
            var Q60;
            Q60=makeQuery(id+"F8.opPattern","COPY",BODY,{"derivedFrom":makeQuery(id+"F6.opPattern","COPY",BODY,{"derivedFrom":makeQuery(id+"F1.opRevolve","SWEPT_BODY",BODY,{"disambiguationData":[OSD([sQuery(id+"F0.wireOp",EDGE,"E1")])]}),"instanceName":"1"}),"instanceName":"1"});
            var Q61;
            Q61=makeQuery(id+"F8.opPattern","COPY",BODY,{"derivedFrom":makeQuery(id+"F6.opPattern","COPY",BODY,{"derivedFrom":makeQuery(id+"F2.opPattern","COPY",BODY,{"derivedFrom":makeQuery(id+"F1.opRevolve","SWEPT_BODY",BODY,{"disambiguationData":[OSD([sQuery(id+"F0.wireOp",EDGE,"E1")])]}),"instanceName":"1"}),"instanceName":"1"}),"instanceName":"1"});
            var Q62;
            Q62=makeQuery(id+"F8.opPattern","COPY",BODY,{"derivedFrom":makeQuery(id+"F6.opPattern","COPY",BODY,{"derivedFrom":makeQuery(id+"F3.opPattern","COPY",BODY,{"derivedFrom":makeQuery(id+"F2.opPattern","COPY",BODY,{"derivedFrom":makeQuery(id+"F1.opRevolve","SWEPT_BODY",BODY,{"disambiguationData":[OSD([sQuery(id+"F0.wireOp",EDGE,"E1")])]}),"instanceName":"1"}),"instanceName":"1"}),"instanceName":"1"}),"instanceName":"1"});
            var Q63;
            Q63=makeQuery(id+"F8.opPattern","COPY",BODY,{"derivedFrom":makeQuery(id+"F6.opPattern","COPY",BODY,{"derivedFrom":makeQuery(id+"F4.opPattern","COPY",BODY,{"derivedFrom":makeQuery(id+"F1.opRevolve","SWEPT_BODY",BODY,{"disambiguationData":[OSD([sQuery(id+"F0.wireOp",EDGE,"E1")])]}),"instanceName":"1"}),"instanceName":"1"}),"instanceName":"1"});
            var Q64;
            Q64=makeQuery(id+"F8.opPattern","COPY",BODY,{"derivedFrom":makeQuery(id+"F6.opPattern","COPY",BODY,{"derivedFrom":makeQuery(id+"F4.opPattern","COPY",BODY,{"derivedFrom":makeQuery(id+"F2.opPattern","COPY",BODY,{"derivedFrom":makeQuery(id+"F1.opRevolve","SWEPT_BODY",BODY,{"disambiguationData":[OSD([sQuery(id+"F0.wireOp",EDGE,"E1")])]}),"instanceName":"1"}),"instanceName":"1"}),"instanceName":"1"}),"instanceName":"1"});
            var Q65;
            Q65=makeQuery(id+"F8.opPattern","COPY",BODY,{"derivedFrom":makeQuery(id+"F6.opPattern","COPY",BODY,{"derivedFrom":makeQuery(id+"F4.opPattern","COPY",BODY,{"derivedFrom":makeQuery(id+"F3.opPattern","COPY",BODY,{"derivedFrom":makeQuery(id+"F2.opPattern","COPY",BODY,{"derivedFrom":makeQuery(id+"F1.opRevolve","SWEPT_BODY",BODY,{"disambiguationData":[OSD([sQuery(id+"F0.wireOp",EDGE,"E1")])]}),"instanceName":"1"}),"instanceName":"1"}),"instanceName":"1"}),"instanceName":"1"}),"instanceName":"1"});
            var Q66;
            Q66=makeQuery(id+"F8.opPattern","COPY",BODY,{"derivedFrom":makeQuery(id+"F6.opPattern","COPY",BODY,{"derivedFrom":makeQuery(id+"F5.opPattern","COPY",BODY,{"derivedFrom":makeQuery(id+"F1.opRevolve","SWEPT_BODY",BODY,{"disambiguationData":[OSD([sQuery(id+"F0.wireOp",EDGE,"E1")])]}),"instanceName":"1"}),"instanceName":"1"}),"instanceName":"1"});
            var Q67;
            Q67=makeQuery(id+"F8.opPattern","COPY",BODY,{"derivedFrom":makeQuery(id+"F6.opPattern","COPY",BODY,{"derivedFrom":makeQuery(id+"F5.opPattern","COPY",BODY,{"derivedFrom":makeQuery(id+"F2.opPattern","COPY",BODY,{"derivedFrom":makeQuery(id+"F1.opRevolve","SWEPT_BODY",BODY,{"disambiguationData":[OSD([sQuery(id+"F0.wireOp",EDGE,"E1")])]}),"instanceName":"1"}),"instanceName":"1"}),"instanceName":"1"}),"instanceName":"1"});
            var Q68;
            Q68=makeQuery(id+"F8.opPattern","COPY",BODY,{"derivedFrom":makeQuery(id+"F6.opPattern","COPY",BODY,{"derivedFrom":makeQuery(id+"F5.opPattern","COPY",BODY,{"derivedFrom":makeQuery(id+"F3.opPattern","COPY",BODY,{"derivedFrom":makeQuery(id+"F2.opPattern","COPY",BODY,{"derivedFrom":makeQuery(id+"F1.opRevolve","SWEPT_BODY",BODY,{"disambiguationData":[OSD([sQuery(id+"F0.wireOp",EDGE,"E1")])]}),"instanceName":"1"}),"instanceName":"1"}),"instanceName":"1"}),"instanceName":"1"}),"instanceName":"1"});
            var Q69;
            Q69=makeQuery(id+"F8.opPattern","COPY",BODY,{"derivedFrom":makeQuery(id+"F6.opPattern","COPY",BODY,{"derivedFrom":makeQuery(id+"F5.opPattern","COPY",BODY,{"derivedFrom":makeQuery(id+"F4.opPattern","COPY",BODY,{"derivedFrom":makeQuery(id+"F1.opRevolve","SWEPT_BODY",BODY,{"disambiguationData":[OSD([sQuery(id+"F0.wireOp",EDGE,"E1")])]}),"instanceName":"1"}),"instanceName":"1"}),"instanceName":"1"}),"instanceName":"1"});
            var Q70;
            Q70=makeQuery(id+"F8.opPattern","COPY",BODY,{"derivedFrom":makeQuery(id+"F6.opPattern","COPY",BODY,{"derivedFrom":makeQuery(id+"F5.opPattern","COPY",BODY,{"derivedFrom":makeQuery(id+"F4.opPattern","COPY",BODY,{"derivedFrom":makeQuery(id+"F2.opPattern","COPY",BODY,{"derivedFrom":makeQuery(id+"F1.opRevolve","SWEPT_BODY",BODY,{"disambiguationData":[OSD([sQuery(id+"F0.wireOp",EDGE,"E1")])]}),"instanceName":"1"}),"instanceName":"1"}),"instanceName":"1"}),"instanceName":"1"}),"instanceName":"1"});
            var Q71;
            Q71=makeQuery(id+"F8.opPattern","COPY",BODY,{"derivedFrom":makeQuery(id+"F6.opPattern","COPY",BODY,{"derivedFrom":makeQuery(id+"F5.opPattern","COPY",BODY,{"derivedFrom":makeQuery(id+"F4.opPattern","COPY",BODY,{"derivedFrom":makeQuery(id+"F3.opPattern","COPY",BODY,{"derivedFrom":makeQuery(id+"F2.opPattern","COPY",BODY,{"derivedFrom":makeQuery(id+"F1.opRevolve","SWEPT_BODY",BODY,{"disambiguationData":[OSD([sQuery(id+"F0.wireOp",EDGE,"E1")])]}),"instanceName":"1"}),"instanceName":"1"}),"instanceName":"1"}),"instanceName":"1"}),"instanceName":"1"}),"instanceName":"1"});
            var Q72;
            Q72=makeQuery(id+"F8.opPattern","COPY",BODY,{"derivedFrom":makeQuery(id+"F7.opPattern","COPY",BODY,{"derivedFrom":makeQuery(id+"F1.opRevolve","SWEPT_BODY",BODY,{"disambiguationData":[OSD([sQuery(id+"F0.wireOp",EDGE,"E1")])]}),"instanceName":"1"}),"instanceName":"1"});
            var Q73;
            Q73=makeQuery(id+"F8.opPattern","COPY",BODY,{"derivedFrom":makeQuery(id+"F7.opPattern","COPY",BODY,{"derivedFrom":makeQuery(id+"F2.opPattern","COPY",BODY,{"derivedFrom":makeQuery(id+"F1.opRevolve","SWEPT_BODY",BODY,{"disambiguationData":[OSD([sQuery(id+"F0.wireOp",EDGE,"E1")])]}),"instanceName":"1"}),"instanceName":"1"}),"instanceName":"1"});
            var Q74;
            Q74=makeQuery(id+"F8.opPattern","COPY",BODY,{"derivedFrom":makeQuery(id+"F7.opPattern","COPY",BODY,{"derivedFrom":makeQuery(id+"F3.opPattern","COPY",BODY,{"derivedFrom":makeQuery(id+"F2.opPattern","COPY",BODY,{"derivedFrom":makeQuery(id+"F1.opRevolve","SWEPT_BODY",BODY,{"disambiguationData":[OSD([sQuery(id+"F0.wireOp",EDGE,"E1")])]}),"instanceName":"1"}),"instanceName":"1"}),"instanceName":"1"}),"instanceName":"1"});
            var Q75;
            Q75=makeQuery(id+"F8.opPattern","COPY",BODY,{"derivedFrom":makeQuery(id+"F7.opPattern","COPY",BODY,{"derivedFrom":makeQuery(id+"F4.opPattern","COPY",BODY,{"derivedFrom":makeQuery(id+"F1.opRevolve","SWEPT_BODY",BODY,{"disambiguationData":[OSD([sQuery(id+"F0.wireOp",EDGE,"E1")])]}),"instanceName":"1"}),"instanceName":"1"}),"instanceName":"1"});
            var Q76;
            Q76=makeQuery(id+"F8.opPattern","COPY",BODY,{"derivedFrom":makeQuery(id+"F7.opPattern","COPY",BODY,{"derivedFrom":makeQuery(id+"F4.opPattern","COPY",BODY,{"derivedFrom":makeQuery(id+"F2.opPattern","COPY",BODY,{"derivedFrom":makeQuery(id+"F1.opRevolve","SWEPT_BODY",BODY,{"disambiguationData":[OSD([sQuery(id+"F0.wireOp",EDGE,"E1")])]}),"instanceName":"1"}),"instanceName":"1"}),"instanceName":"1"}),"instanceName":"1"});
            var Q77;
            Q77=makeQuery(id+"F8.opPattern","COPY",BODY,{"derivedFrom":makeQuery(id+"F7.opPattern","COPY",BODY,{"derivedFrom":makeQuery(id+"F4.opPattern","COPY",BODY,{"derivedFrom":makeQuery(id+"F3.opPattern","COPY",BODY,{"derivedFrom":makeQuery(id+"F2.opPattern","COPY",BODY,{"derivedFrom":makeQuery(id+"F1.opRevolve","SWEPT_BODY",BODY,{"disambiguationData":[OSD([sQuery(id+"F0.wireOp",EDGE,"E1")])]}),"instanceName":"1"}),"instanceName":"1"}),"instanceName":"1"}),"instanceName":"1"}),"instanceName":"1"});
            var Q78;
            Q78=makeQuery(id+"F8.opPattern","COPY",BODY,{"derivedFrom":makeQuery(id+"F7.opPattern","COPY",BODY,{"derivedFrom":makeQuery(id+"F5.opPattern","COPY",BODY,{"derivedFrom":makeQuery(id+"F1.opRevolve","SWEPT_BODY",BODY,{"disambiguationData":[OSD([sQuery(id+"F0.wireOp",EDGE,"E1")])]}),"instanceName":"1"}),"instanceName":"1"}),"instanceName":"1"});
            var Q79;
            Q79=makeQuery(id+"F8.opPattern","COPY",BODY,{"derivedFrom":makeQuery(id+"F7.opPattern","COPY",BODY,{"derivedFrom":makeQuery(id+"F5.opPattern","COPY",BODY,{"derivedFrom":makeQuery(id+"F2.opPattern","COPY",BODY,{"derivedFrom":makeQuery(id+"F1.opRevolve","SWEPT_BODY",BODY,{"disambiguationData":[OSD([sQuery(id+"F0.wireOp",EDGE,"E1")])]}),"instanceName":"1"}),"instanceName":"1"}),"instanceName":"1"}),"instanceName":"1"});
            var Q80;
            Q80=makeQuery(id+"F8.opPattern","COPY",BODY,{"derivedFrom":makeQuery(id+"F7.opPattern","COPY",BODY,{"derivedFrom":makeQuery(id+"F5.opPattern","COPY",BODY,{"derivedFrom":makeQuery(id+"F3.opPattern","COPY",BODY,{"derivedFrom":makeQuery(id+"F2.opPattern","COPY",BODY,{"derivedFrom":makeQuery(id+"F1.opRevolve","SWEPT_BODY",BODY,{"disambiguationData":[OSD([sQuery(id+"F0.wireOp",EDGE,"E1")])]}),"instanceName":"1"}),"instanceName":"1"}),"instanceName":"1"}),"instanceName":"1"}),"instanceName":"1"});
            var Q81;
            Q81=makeQuery(id+"F8.opPattern","COPY",BODY,{"derivedFrom":makeQuery(id+"F7.opPattern","COPY",BODY,{"derivedFrom":makeQuery(id+"F5.opPattern","COPY",BODY,{"derivedFrom":makeQuery(id+"F4.opPattern","COPY",BODY,{"derivedFrom":makeQuery(id+"F1.opRevolve","SWEPT_BODY",BODY,{"disambiguationData":[OSD([sQuery(id+"F0.wireOp",EDGE,"E1")])]}),"instanceName":"1"}),"instanceName":"1"}),"instanceName":"1"}),"instanceName":"1"});
            var Q82;
            Q82=makeQuery(id+"F8.opPattern","COPY",BODY,{"derivedFrom":makeQuery(id+"F7.opPattern","COPY",BODY,{"derivedFrom":makeQuery(id+"F5.opPattern","COPY",BODY,{"derivedFrom":makeQuery(id+"F4.opPattern","COPY",BODY,{"derivedFrom":makeQuery(id+"F2.opPattern","COPY",BODY,{"derivedFrom":makeQuery(id+"F1.opRevolve","SWEPT_BODY",BODY,{"disambiguationData":[OSD([sQuery(id+"F0.wireOp",EDGE,"E1")])]}),"instanceName":"1"}),"instanceName":"1"}),"instanceName":"1"}),"instanceName":"1"}),"instanceName":"1"});
            var Q83;
            Q83=makeQuery(id+"F8.opPattern","COPY",BODY,{"derivedFrom":makeQuery(id+"F7.opPattern","COPY",BODY,{"derivedFrom":makeQuery(id+"F5.opPattern","COPY",BODY,{"derivedFrom":makeQuery(id+"F4.opPattern","COPY",BODY,{"derivedFrom":makeQuery(id+"F3.opPattern","COPY",BODY,{"derivedFrom":makeQuery(id+"F2.opPattern","COPY",BODY,{"derivedFrom":makeQuery(id+"F1.opRevolve","SWEPT_BODY",BODY,{"disambiguationData":[OSD([sQuery(id+"F0.wireOp",EDGE,"E1")])]}),"instanceName":"1"}),"instanceName":"1"}),"instanceName":"1"}),"instanceName":"1"}),"instanceName":"1"}),"instanceName":"1"});
            var Q84;
            Q84=makeQuery(id+"F8.opPattern","COPY",BODY,{"derivedFrom":makeQuery(id+"F7.opPattern","COPY",BODY,{"derivedFrom":makeQuery(id+"F6.opPattern","COPY",BODY,{"derivedFrom":makeQuery(id+"F1.opRevolve","SWEPT_BODY",BODY,{"disambiguationData":[OSD([sQuery(id+"F0.wireOp",EDGE,"E1")])]}),"instanceName":"1"}),"instanceName":"1"}),"instanceName":"1"});
            var Q85;
            Q85=makeQuery(id+"F8.opPattern","COPY",BODY,{"derivedFrom":makeQuery(id+"F7.opPattern","COPY",BODY,{"derivedFrom":makeQuery(id+"F6.opPattern","COPY",BODY,{"derivedFrom":makeQuery(id+"F2.opPattern","COPY",BODY,{"derivedFrom":makeQuery(id+"F1.opRevolve","SWEPT_BODY",BODY,{"disambiguationData":[OSD([sQuery(id+"F0.wireOp",EDGE,"E1")])]}),"instanceName":"1"}),"instanceName":"1"}),"instanceName":"1"}),"instanceName":"1"});
            var Q86;
            Q86=makeQuery(id+"F8.opPattern","COPY",BODY,{"derivedFrom":makeQuery(id+"F7.opPattern","COPY",BODY,{"derivedFrom":makeQuery(id+"F6.opPattern","COPY",BODY,{"derivedFrom":makeQuery(id+"F3.opPattern","COPY",BODY,{"derivedFrom":makeQuery(id+"F2.opPattern","COPY",BODY,{"derivedFrom":makeQuery(id+"F1.opRevolve","SWEPT_BODY",BODY,{"disambiguationData":[OSD([sQuery(id+"F0.wireOp",EDGE,"E1")])]}),"instanceName":"1"}),"instanceName":"1"}),"instanceName":"1"}),"instanceName":"1"}),"instanceName":"1"});
            var Q87;
            Q87=makeQuery(id+"F8.opPattern","COPY",BODY,{"derivedFrom":makeQuery(id+"F7.opPattern","COPY",BODY,{"derivedFrom":makeQuery(id+"F6.opPattern","COPY",BODY,{"derivedFrom":makeQuery(id+"F4.opPattern","COPY",BODY,{"derivedFrom":makeQuery(id+"F1.opRevolve","SWEPT_BODY",BODY,{"disambiguationData":[OSD([sQuery(id+"F0.wireOp",EDGE,"E1")])]}),"instanceName":"1"}),"instanceName":"1"}),"instanceName":"1"}),"instanceName":"1"});
            var Q88;
            Q88=makeQuery(id+"F8.opPattern","COPY",BODY,{"derivedFrom":makeQuery(id+"F7.opPattern","COPY",BODY,{"derivedFrom":makeQuery(id+"F6.opPattern","COPY",BODY,{"derivedFrom":makeQuery(id+"F4.opPattern","COPY",BODY,{"derivedFrom":makeQuery(id+"F2.opPattern","COPY",BODY,{"derivedFrom":makeQuery(id+"F1.opRevolve","SWEPT_BODY",BODY,{"disambiguationData":[OSD([sQuery(id+"F0.wireOp",EDGE,"E1")])]}),"instanceName":"1"}),"instanceName":"1"}),"instanceName":"1"}),"instanceName":"1"}),"instanceName":"1"});
            var Q89;
            Q89=makeQuery(id+"F8.opPattern","COPY",BODY,{"derivedFrom":makeQuery(id+"F7.opPattern","COPY",BODY,{"derivedFrom":makeQuery(id+"F6.opPattern","COPY",BODY,{"derivedFrom":makeQuery(id+"F4.opPattern","COPY",BODY,{"derivedFrom":makeQuery(id+"F3.opPattern","COPY",BODY,{"derivedFrom":makeQuery(id+"F2.opPattern","COPY",BODY,{"derivedFrom":makeQuery(id+"F1.opRevolve","SWEPT_BODY",BODY,{"disambiguationData":[OSD([sQuery(id+"F0.wireOp",EDGE,"E1")])]}),"instanceName":"1"}),"instanceName":"1"}),"instanceName":"1"}),"instanceName":"1"}),"instanceName":"1"}),"instanceName":"1"});
            var Q90;
            Q90=makeQuery(id+"F8.opPattern","COPY",BODY,{"derivedFrom":makeQuery(id+"F7.opPattern","COPY",BODY,{"derivedFrom":makeQuery(id+"F6.opPattern","COPY",BODY,{"derivedFrom":makeQuery(id+"F5.opPattern","COPY",BODY,{"derivedFrom":makeQuery(id+"F1.opRevolve","SWEPT_BODY",BODY,{"disambiguationData":[OSD([sQuery(id+"F0.wireOp",EDGE,"E1")])]}),"instanceName":"1"}),"instanceName":"1"}),"instanceName":"1"}),"instanceName":"1"});
            var Q91;
            Q91=makeQuery(id+"F8.opPattern","COPY",BODY,{"derivedFrom":makeQuery(id+"F7.opPattern","COPY",BODY,{"derivedFrom":makeQuery(id+"F6.opPattern","COPY",BODY,{"derivedFrom":makeQuery(id+"F5.opPattern","COPY",BODY,{"derivedFrom":makeQuery(id+"F2.opPattern","COPY",BODY,{"derivedFrom":makeQuery(id+"F1.opRevolve","SWEPT_BODY",BODY,{"disambiguationData":[OSD([sQuery(id+"F0.wireOp",EDGE,"E1")])]}),"instanceName":"1"}),"instanceName":"1"}),"instanceName":"1"}),"instanceName":"1"}),"instanceName":"1"});
            var Q92;
            Q92=makeQuery(id+"F8.opPattern","COPY",BODY,{"derivedFrom":makeQuery(id+"F7.opPattern","COPY",BODY,{"derivedFrom":makeQuery(id+"F6.opPattern","COPY",BODY,{"derivedFrom":makeQuery(id+"F5.opPattern","COPY",BODY,{"derivedFrom":makeQuery(id+"F3.opPattern","COPY",BODY,{"derivedFrom":makeQuery(id+"F2.opPattern","COPY",BODY,{"derivedFrom":makeQuery(id+"F1.opRevolve","SWEPT_BODY",BODY,{"disambiguationData":[OSD([sQuery(id+"F0.wireOp",EDGE,"E1")])]}),"instanceName":"1"}),"instanceName":"1"}),"instanceName":"1"}),"instanceName":"1"}),"instanceName":"1"}),"instanceName":"1"});
            var Q93;
            Q93=makeQuery(id+"F8.opPattern","COPY",BODY,{"derivedFrom":makeQuery(id+"F7.opPattern","COPY",BODY,{"derivedFrom":makeQuery(id+"F6.opPattern","COPY",BODY,{"derivedFrom":makeQuery(id+"F5.opPattern","COPY",BODY,{"derivedFrom":makeQuery(id+"F4.opPattern","COPY",BODY,{"derivedFrom":makeQuery(id+"F1.opRevolve","SWEPT_BODY",BODY,{"disambiguationData":[OSD([sQuery(id+"F0.wireOp",EDGE,"E1")])]}),"instanceName":"1"}),"instanceName":"1"}),"instanceName":"1"}),"instanceName":"1"}),"instanceName":"1"});
            var Q94;
            Q94=makeQuery(id+"F8.opPattern","COPY",BODY,{"derivedFrom":makeQuery(id+"F7.opPattern","COPY",BODY,{"derivedFrom":makeQuery(id+"F6.opPattern","COPY",BODY,{"derivedFrom":makeQuery(id+"F5.opPattern","COPY",BODY,{"derivedFrom":makeQuery(id+"F4.opPattern","COPY",BODY,{"derivedFrom":makeQuery(id+"F2.opPattern","COPY",BODY,{"derivedFrom":makeQuery(id+"F1.opRevolve","SWEPT_BODY",BODY,{"disambiguationData":[OSD([sQuery(id+"F0.wireOp",EDGE,"E1")])]}),"instanceName":"1"}),"instanceName":"1"}),"instanceName":"1"}),"instanceName":"1"}),"instanceName":"1"}),"instanceName":"1"});
            var Q95;
            Q95=makeQuery(id+"F8.opPattern","COPY",BODY,{"derivedFrom":makeQuery(id+"F7.opPattern","COPY",BODY,{"derivedFrom":makeQuery(id+"F6.opPattern","COPY",BODY,{"derivedFrom":makeQuery(id+"F5.opPattern","COPY",BODY,{"derivedFrom":makeQuery(id+"F4.opPattern","COPY",BODY,{"derivedFrom":makeQuery(id+"F3.opPattern","COPY",BODY,{"derivedFrom":makeQuery(id+"F2.opPattern","COPY",BODY,{"derivedFrom":makeQuery(id+"F1.opRevolve","SWEPT_BODY",BODY,{"disambiguationData":[OSD([sQuery(id+"F0.wireOp",EDGE,"E1")])]}),"instanceName":"1"}),"instanceName":"1"}),"instanceName":"1"}),"instanceName":"1"}),"instanceName":"1"}),"instanceName":"1"}),"instanceName":"1"});
            var Q96;
            Q96=makeQuery(id+"F9.opPattern","COPY",BODY,{"derivedFrom":makeQuery(id+"F1.opRevolve","SWEPT_BODY",BODY,{"disambiguationData":[OSD([sQuery(id+"F0.wireOp",EDGE,"E1")])]}),"instanceName":"1"});
            var Q97;
            Q97=makeQuery(id+"F9.opPattern","COPY",BODY,{"derivedFrom":makeQuery(id+"F2.opPattern","COPY",BODY,{"derivedFrom":makeQuery(id+"F1.opRevolve","SWEPT_BODY",BODY,{"disambiguationData":[OSD([sQuery(id+"F0.wireOp",EDGE,"E1")])]}),"instanceName":"1"}),"instanceName":"1"});
            var Q98;
            Q98=makeQuery(id+"F9.opPattern","COPY",BODY,{"derivedFrom":makeQuery(id+"F3.opPattern","COPY",BODY,{"derivedFrom":makeQuery(id+"F2.opPattern","COPY",BODY,{"derivedFrom":makeQuery(id+"F1.opRevolve","SWEPT_BODY",BODY,{"disambiguationData":[OSD([sQuery(id+"F0.wireOp",EDGE,"E1")])]}),"instanceName":"1"}),"instanceName":"1"}),"instanceName":"1"});
            var Q99;
            Q99=makeQuery(id+"F9.opPattern","COPY",BODY,{"derivedFrom":makeQuery(id+"F4.opPattern","COPY",BODY,{"derivedFrom":makeQuery(id+"F1.opRevolve","SWEPT_BODY",BODY,{"disambiguationData":[OSD([sQuery(id+"F0.wireOp",EDGE,"E1")])]}),"instanceName":"1"}),"instanceName":"1"});
            var Q100;
            Q100=makeQuery(id+"F9.opPattern","COPY",BODY,{"derivedFrom":makeQuery(id+"F4.opPattern","COPY",BODY,{"derivedFrom":makeQuery(id+"F2.opPattern","COPY",BODY,{"derivedFrom":makeQuery(id+"F1.opRevolve","SWEPT_BODY",BODY,{"disambiguationData":[OSD([sQuery(id+"F0.wireOp",EDGE,"E1")])]}),"instanceName":"1"}),"instanceName":"1"}),"instanceName":"1"});
            var Q101;
            Q101=makeQuery(id+"F9.opPattern","COPY",BODY,{"derivedFrom":makeQuery(id+"F4.opPattern","COPY",BODY,{"derivedFrom":makeQuery(id+"F3.opPattern","COPY",BODY,{"derivedFrom":makeQuery(id+"F2.opPattern","COPY",BODY,{"derivedFrom":makeQuery(id+"F1.opRevolve","SWEPT_BODY",BODY,{"disambiguationData":[OSD([sQuery(id+"F0.wireOp",EDGE,"E1")])]}),"instanceName":"1"}),"instanceName":"1"}),"instanceName":"1"}),"instanceName":"1"});
            var Q102;
            Q102=makeQuery(id+"F9.opPattern","COPY",BODY,{"derivedFrom":makeQuery(id+"F5.opPattern","COPY",BODY,{"derivedFrom":makeQuery(id+"F1.opRevolve","SWEPT_BODY",BODY,{"disambiguationData":[OSD([sQuery(id+"F0.wireOp",EDGE,"E1")])]}),"instanceName":"1"}),"instanceName":"1"});
            var Q103;
            Q103=makeQuery(id+"F9.opPattern","COPY",BODY,{"derivedFrom":makeQuery(id+"F5.opPattern","COPY",BODY,{"derivedFrom":makeQuery(id+"F2.opPattern","COPY",BODY,{"derivedFrom":makeQuery(id+"F1.opRevolve","SWEPT_BODY",BODY,{"disambiguationData":[OSD([sQuery(id+"F0.wireOp",EDGE,"E1")])]}),"instanceName":"1"}),"instanceName":"1"}),"instanceName":"1"});
            var Q104;
            Q104=makeQuery(id+"F9.opPattern","COPY",BODY,{"derivedFrom":makeQuery(id+"F5.opPattern","COPY",BODY,{"derivedFrom":makeQuery(id+"F3.opPattern","COPY",BODY,{"derivedFrom":makeQuery(id+"F2.opPattern","COPY",BODY,{"derivedFrom":makeQuery(id+"F1.opRevolve","SWEPT_BODY",BODY,{"disambiguationData":[OSD([sQuery(id+"F0.wireOp",EDGE,"E1")])]}),"instanceName":"1"}),"instanceName":"1"}),"instanceName":"1"}),"instanceName":"1"});
            var Q105;
            Q105=makeQuery(id+"F9.opPattern","COPY",BODY,{"derivedFrom":makeQuery(id+"F5.opPattern","COPY",BODY,{"derivedFrom":makeQuery(id+"F4.opPattern","COPY",BODY,{"derivedFrom":makeQuery(id+"F1.opRevolve","SWEPT_BODY",BODY,{"disambiguationData":[OSD([sQuery(id+"F0.wireOp",EDGE,"E1")])]}),"instanceName":"1"}),"instanceName":"1"}),"instanceName":"1"});
            var Q106;
            Q106=makeQuery(id+"F9.opPattern","COPY",BODY,{"derivedFrom":makeQuery(id+"F5.opPattern","COPY",BODY,{"derivedFrom":makeQuery(id+"F4.opPattern","COPY",BODY,{"derivedFrom":makeQuery(id+"F2.opPattern","COPY",BODY,{"derivedFrom":makeQuery(id+"F1.opRevolve","SWEPT_BODY",BODY,{"disambiguationData":[OSD([sQuery(id+"F0.wireOp",EDGE,"E1")])]}),"instanceName":"1"}),"instanceName":"1"}),"instanceName":"1"}),"instanceName":"1"});
            var Q107;
            Q107=makeQuery(id+"F9.opPattern","COPY",BODY,{"derivedFrom":makeQuery(id+"F5.opPattern","COPY",BODY,{"derivedFrom":makeQuery(id+"F4.opPattern","COPY",BODY,{"derivedFrom":makeQuery(id+"F3.opPattern","COPY",BODY,{"derivedFrom":makeQuery(id+"F2.opPattern","COPY",BODY,{"derivedFrom":makeQuery(id+"F1.opRevolve","SWEPT_BODY",BODY,{"disambiguationData":[OSD([sQuery(id+"F0.wireOp",EDGE,"E1")])]}),"instanceName":"1"}),"instanceName":"1"}),"instanceName":"1"}),"instanceName":"1"}),"instanceName":"1"});
            var Q108;
            Q108=makeQuery(id+"F9.opPattern","COPY",BODY,{"derivedFrom":makeQuery(id+"F6.opPattern","COPY",BODY,{"derivedFrom":makeQuery(id+"F1.opRevolve","SWEPT_BODY",BODY,{"disambiguationData":[OSD([sQuery(id+"F0.wireOp",EDGE,"E1")])]}),"instanceName":"1"}),"instanceName":"1"});
            var Q109;
            Q109=makeQuery(id+"F9.opPattern","COPY",BODY,{"derivedFrom":makeQuery(id+"F6.opPattern","COPY",BODY,{"derivedFrom":makeQuery(id+"F2.opPattern","COPY",BODY,{"derivedFrom":makeQuery(id+"F1.opRevolve","SWEPT_BODY",BODY,{"disambiguationData":[OSD([sQuery(id+"F0.wireOp",EDGE,"E1")])]}),"instanceName":"1"}),"instanceName":"1"}),"instanceName":"1"});
            var Q110;
            Q110=makeQuery(id+"F9.opPattern","COPY",BODY,{"derivedFrom":makeQuery(id+"F6.opPattern","COPY",BODY,{"derivedFrom":makeQuery(id+"F3.opPattern","COPY",BODY,{"derivedFrom":makeQuery(id+"F2.opPattern","COPY",BODY,{"derivedFrom":makeQuery(id+"F1.opRevolve","SWEPT_BODY",BODY,{"disambiguationData":[OSD([sQuery(id+"F0.wireOp",EDGE,"E1")])]}),"instanceName":"1"}),"instanceName":"1"}),"instanceName":"1"}),"instanceName":"1"});
            var Q111;
            Q111=makeQuery(id+"F9.opPattern","COPY",BODY,{"derivedFrom":makeQuery(id+"F6.opPattern","COPY",BODY,{"derivedFrom":makeQuery(id+"F4.opPattern","COPY",BODY,{"derivedFrom":makeQuery(id+"F1.opRevolve","SWEPT_BODY",BODY,{"disambiguationData":[OSD([sQuery(id+"F0.wireOp",EDGE,"E1")])]}),"instanceName":"1"}),"instanceName":"1"}),"instanceName":"1"});
            var Q112;
            Q112=makeQuery(id+"F9.opPattern","COPY",BODY,{"derivedFrom":makeQuery(id+"F6.opPattern","COPY",BODY,{"derivedFrom":makeQuery(id+"F4.opPattern","COPY",BODY,{"derivedFrom":makeQuery(id+"F2.opPattern","COPY",BODY,{"derivedFrom":makeQuery(id+"F1.opRevolve","SWEPT_BODY",BODY,{"disambiguationData":[OSD([sQuery(id+"F0.wireOp",EDGE,"E1")])]}),"instanceName":"1"}),"instanceName":"1"}),"instanceName":"1"}),"instanceName":"1"});
            var Q113;
            Q113=makeQuery(id+"F9.opPattern","COPY",BODY,{"derivedFrom":makeQuery(id+"F6.opPattern","COPY",BODY,{"derivedFrom":makeQuery(id+"F4.opPattern","COPY",BODY,{"derivedFrom":makeQuery(id+"F3.opPattern","COPY",BODY,{"derivedFrom":makeQuery(id+"F2.opPattern","COPY",BODY,{"derivedFrom":makeQuery(id+"F1.opRevolve","SWEPT_BODY",BODY,{"disambiguationData":[OSD([sQuery(id+"F0.wireOp",EDGE,"E1")])]}),"instanceName":"1"}),"instanceName":"1"}),"instanceName":"1"}),"instanceName":"1"}),"instanceName":"1"});
            var Q114;
            Q114=makeQuery(id+"F9.opPattern","COPY",BODY,{"derivedFrom":makeQuery(id+"F6.opPattern","COPY",BODY,{"derivedFrom":makeQuery(id+"F5.opPattern","COPY",BODY,{"derivedFrom":makeQuery(id+"F1.opRevolve","SWEPT_BODY",BODY,{"disambiguationData":[OSD([sQuery(id+"F0.wireOp",EDGE,"E1")])]}),"instanceName":"1"}),"instanceName":"1"}),"instanceName":"1"});
            var Q115;
            Q115=makeQuery(id+"F9.opPattern","COPY",BODY,{"derivedFrom":makeQuery(id+"F6.opPattern","COPY",BODY,{"derivedFrom":makeQuery(id+"F5.opPattern","COPY",BODY,{"derivedFrom":makeQuery(id+"F2.opPattern","COPY",BODY,{"derivedFrom":makeQuery(id+"F1.opRevolve","SWEPT_BODY",BODY,{"disambiguationData":[OSD([sQuery(id+"F0.wireOp",EDGE,"E1")])]}),"instanceName":"1"}),"instanceName":"1"}),"instanceName":"1"}),"instanceName":"1"});
            var Q116;
            Q116=makeQuery(id+"F9.opPattern","COPY",BODY,{"derivedFrom":makeQuery(id+"F6.opPattern","COPY",BODY,{"derivedFrom":makeQuery(id+"F5.opPattern","COPY",BODY,{"derivedFrom":makeQuery(id+"F3.opPattern","COPY",BODY,{"derivedFrom":makeQuery(id+"F2.opPattern","COPY",BODY,{"derivedFrom":makeQuery(id+"F1.opRevolve","SWEPT_BODY",BODY,{"disambiguationData":[OSD([sQuery(id+"F0.wireOp",EDGE,"E1")])]}),"instanceName":"1"}),"instanceName":"1"}),"instanceName":"1"}),"instanceName":"1"}),"instanceName":"1"});
            var Q117;
            Q117=makeQuery(id+"F9.opPattern","COPY",BODY,{"derivedFrom":makeQuery(id+"F6.opPattern","COPY",BODY,{"derivedFrom":makeQuery(id+"F5.opPattern","COPY",BODY,{"derivedFrom":makeQuery(id+"F4.opPattern","COPY",BODY,{"derivedFrom":makeQuery(id+"F1.opRevolve","SWEPT_BODY",BODY,{"disambiguationData":[OSD([sQuery(id+"F0.wireOp",EDGE,"E1")])]}),"instanceName":"1"}),"instanceName":"1"}),"instanceName":"1"}),"instanceName":"1"});
            var Q118;
            Q118=makeQuery(id+"F9.opPattern","COPY",BODY,{"derivedFrom":makeQuery(id+"F6.opPattern","COPY",BODY,{"derivedFrom":makeQuery(id+"F5.opPattern","COPY",BODY,{"derivedFrom":makeQuery(id+"F4.opPattern","COPY",BODY,{"derivedFrom":makeQuery(id+"F2.opPattern","COPY",BODY,{"derivedFrom":makeQuery(id+"F1.opRevolve","SWEPT_BODY",BODY,{"disambiguationData":[OSD([sQuery(id+"F0.wireOp",EDGE,"E1")])]}),"instanceName":"1"}),"instanceName":"1"}),"instanceName":"1"}),"instanceName":"1"}),"instanceName":"1"});
            var Q119;
            Q119=makeQuery(id+"F9.opPattern","COPY",BODY,{"derivedFrom":makeQuery(id+"F6.opPattern","COPY",BODY,{"derivedFrom":makeQuery(id+"F5.opPattern","COPY",BODY,{"derivedFrom":makeQuery(id+"F4.opPattern","COPY",BODY,{"derivedFrom":makeQuery(id+"F3.opPattern","COPY",BODY,{"derivedFrom":makeQuery(id+"F2.opPattern","COPY",BODY,{"derivedFrom":makeQuery(id+"F1.opRevolve","SWEPT_BODY",BODY,{"disambiguationData":[OSD([sQuery(id+"F0.wireOp",EDGE,"E1")])]}),"instanceName":"1"}),"instanceName":"1"}),"instanceName":"1"}),"instanceName":"1"}),"instanceName":"1"}),"instanceName":"1"});
            var Q120;
            Q120=makeQuery(id+"F9.opPattern","COPY",BODY,{"derivedFrom":makeQuery(id+"F7.opPattern","COPY",BODY,{"derivedFrom":makeQuery(id+"F1.opRevolve","SWEPT_BODY",BODY,{"disambiguationData":[OSD([sQuery(id+"F0.wireOp",EDGE,"E1")])]}),"instanceName":"1"}),"instanceName":"1"});
            var Q121;
            Q121=makeQuery(id+"F9.opPattern","COPY",BODY,{"derivedFrom":makeQuery(id+"F7.opPattern","COPY",BODY,{"derivedFrom":makeQuery(id+"F2.opPattern","COPY",BODY,{"derivedFrom":makeQuery(id+"F1.opRevolve","SWEPT_BODY",BODY,{"disambiguationData":[OSD([sQuery(id+"F0.wireOp",EDGE,"E1")])]}),"instanceName":"1"}),"instanceName":"1"}),"instanceName":"1"});
            var Q122;
            Q122=makeQuery(id+"F9.opPattern","COPY",BODY,{"derivedFrom":makeQuery(id+"F7.opPattern","COPY",BODY,{"derivedFrom":makeQuery(id+"F3.opPattern","COPY",BODY,{"derivedFrom":makeQuery(id+"F2.opPattern","COPY",BODY,{"derivedFrom":makeQuery(id+"F1.opRevolve","SWEPT_BODY",BODY,{"disambiguationData":[OSD([sQuery(id+"F0.wireOp",EDGE,"E1")])]}),"instanceName":"1"}),"instanceName":"1"}),"instanceName":"1"}),"instanceName":"1"});
            var Q123;
            Q123=makeQuery(id+"F9.opPattern","COPY",BODY,{"derivedFrom":makeQuery(id+"F7.opPattern","COPY",BODY,{"derivedFrom":makeQuery(id+"F4.opPattern","COPY",BODY,{"derivedFrom":makeQuery(id+"F1.opRevolve","SWEPT_BODY",BODY,{"disambiguationData":[OSD([sQuery(id+"F0.wireOp",EDGE,"E1")])]}),"instanceName":"1"}),"instanceName":"1"}),"instanceName":"1"});
            var Q124;
            Q124=makeQuery(id+"F9.opPattern","COPY",BODY,{"derivedFrom":makeQuery(id+"F7.opPattern","COPY",BODY,{"derivedFrom":makeQuery(id+"F4.opPattern","COPY",BODY,{"derivedFrom":makeQuery(id+"F2.opPattern","COPY",BODY,{"derivedFrom":makeQuery(id+"F1.opRevolve","SWEPT_BODY",BODY,{"disambiguationData":[OSD([sQuery(id+"F0.wireOp",EDGE,"E1")])]}),"instanceName":"1"}),"instanceName":"1"}),"instanceName":"1"}),"instanceName":"1"});
            var Q125;
            Q125=makeQuery(id+"F9.opPattern","COPY",BODY,{"derivedFrom":makeQuery(id+"F7.opPattern","COPY",BODY,{"derivedFrom":makeQuery(id+"F4.opPattern","COPY",BODY,{"derivedFrom":makeQuery(id+"F3.opPattern","COPY",BODY,{"derivedFrom":makeQuery(id+"F2.opPattern","COPY",BODY,{"derivedFrom":makeQuery(id+"F1.opRevolve","SWEPT_BODY",BODY,{"disambiguationData":[OSD([sQuery(id+"F0.wireOp",EDGE,"E1")])]}),"instanceName":"1"}),"instanceName":"1"}),"instanceName":"1"}),"instanceName":"1"}),"instanceName":"1"});
            var Q126;
            Q126=makeQuery(id+"F9.opPattern","COPY",BODY,{"derivedFrom":makeQuery(id+"F7.opPattern","COPY",BODY,{"derivedFrom":makeQuery(id+"F5.opPattern","COPY",BODY,{"derivedFrom":makeQuery(id+"F1.opRevolve","SWEPT_BODY",BODY,{"disambiguationData":[OSD([sQuery(id+"F0.wireOp",EDGE,"E1")])]}),"instanceName":"1"}),"instanceName":"1"}),"instanceName":"1"});
            var Q127;
            Q127=makeQuery(id+"F9.opPattern","COPY",BODY,{"derivedFrom":makeQuery(id+"F7.opPattern","COPY",BODY,{"derivedFrom":makeQuery(id+"F5.opPattern","COPY",BODY,{"derivedFrom":makeQuery(id+"F2.opPattern","COPY",BODY,{"derivedFrom":makeQuery(id+"F1.opRevolve","SWEPT_BODY",BODY,{"disambiguationData":[OSD([sQuery(id+"F0.wireOp",EDGE,"E1")])]}),"instanceName":"1"}),"instanceName":"1"}),"instanceName":"1"}),"instanceName":"1"});
            var Q128;
            Q128=makeQuery(id+"F9.opPattern","COPY",BODY,{"derivedFrom":makeQuery(id+"F7.opPattern","COPY",BODY,{"derivedFrom":makeQuery(id+"F5.opPattern","COPY",BODY,{"derivedFrom":makeQuery(id+"F3.opPattern","COPY",BODY,{"derivedFrom":makeQuery(id+"F2.opPattern","COPY",BODY,{"derivedFrom":makeQuery(id+"F1.opRevolve","SWEPT_BODY",BODY,{"disambiguationData":[OSD([sQuery(id+"F0.wireOp",EDGE,"E1")])]}),"instanceName":"1"}),"instanceName":"1"}),"instanceName":"1"}),"instanceName":"1"}),"instanceName":"1"});
            var Q129;
            Q129=makeQuery(id+"F9.opPattern","COPY",BODY,{"derivedFrom":makeQuery(id+"F7.opPattern","COPY",BODY,{"derivedFrom":makeQuery(id+"F5.opPattern","COPY",BODY,{"derivedFrom":makeQuery(id+"F4.opPattern","COPY",BODY,{"derivedFrom":makeQuery(id+"F1.opRevolve","SWEPT_BODY",BODY,{"disambiguationData":[OSD([sQuery(id+"F0.wireOp",EDGE,"E1")])]}),"instanceName":"1"}),"instanceName":"1"}),"instanceName":"1"}),"instanceName":"1"});
            var Q130;
            Q130=makeQuery(id+"F9.opPattern","COPY",BODY,{"derivedFrom":makeQuery(id+"F7.opPattern","COPY",BODY,{"derivedFrom":makeQuery(id+"F5.opPattern","COPY",BODY,{"derivedFrom":makeQuery(id+"F4.opPattern","COPY",BODY,{"derivedFrom":makeQuery(id+"F2.opPattern","COPY",BODY,{"derivedFrom":makeQuery(id+"F1.opRevolve","SWEPT_BODY",BODY,{"disambiguationData":[OSD([sQuery(id+"F0.wireOp",EDGE,"E1")])]}),"instanceName":"1"}),"instanceName":"1"}),"instanceName":"1"}),"instanceName":"1"}),"instanceName":"1"});
            var Q131;
            Q131=makeQuery(id+"F9.opPattern","COPY",BODY,{"derivedFrom":makeQuery(id+"F7.opPattern","COPY",BODY,{"derivedFrom":makeQuery(id+"F5.opPattern","COPY",BODY,{"derivedFrom":makeQuery(id+"F4.opPattern","COPY",BODY,{"derivedFrom":makeQuery(id+"F3.opPattern","COPY",BODY,{"derivedFrom":makeQuery(id+"F2.opPattern","COPY",BODY,{"derivedFrom":makeQuery(id+"F1.opRevolve","SWEPT_BODY",BODY,{"disambiguationData":[OSD([sQuery(id+"F0.wireOp",EDGE,"E1")])]}),"instanceName":"1"}),"instanceName":"1"}),"instanceName":"1"}),"instanceName":"1"}),"instanceName":"1"}),"instanceName":"1"});
            var Q132;
            Q132=makeQuery(id+"F9.opPattern","COPY",BODY,{"derivedFrom":makeQuery(id+"F7.opPattern","COPY",BODY,{"derivedFrom":makeQuery(id+"F6.opPattern","COPY",BODY,{"derivedFrom":makeQuery(id+"F1.opRevolve","SWEPT_BODY",BODY,{"disambiguationData":[OSD([sQuery(id+"F0.wireOp",EDGE,"E1")])]}),"instanceName":"1"}),"instanceName":"1"}),"instanceName":"1"});
            var Q133;
            Q133=makeQuery(id+"F9.opPattern","COPY",BODY,{"derivedFrom":makeQuery(id+"F7.opPattern","COPY",BODY,{"derivedFrom":makeQuery(id+"F6.opPattern","COPY",BODY,{"derivedFrom":makeQuery(id+"F2.opPattern","COPY",BODY,{"derivedFrom":makeQuery(id+"F1.opRevolve","SWEPT_BODY",BODY,{"disambiguationData":[OSD([sQuery(id+"F0.wireOp",EDGE,"E1")])]}),"instanceName":"1"}),"instanceName":"1"}),"instanceName":"1"}),"instanceName":"1"});
            var Q134;
            Q134=makeQuery(id+"F9.opPattern","COPY",BODY,{"derivedFrom":makeQuery(id+"F7.opPattern","COPY",BODY,{"derivedFrom":makeQuery(id+"F6.opPattern","COPY",BODY,{"derivedFrom":makeQuery(id+"F3.opPattern","COPY",BODY,{"derivedFrom":makeQuery(id+"F2.opPattern","COPY",BODY,{"derivedFrom":makeQuery(id+"F1.opRevolve","SWEPT_BODY",BODY,{"disambiguationData":[OSD([sQuery(id+"F0.wireOp",EDGE,"E1")])]}),"instanceName":"1"}),"instanceName":"1"}),"instanceName":"1"}),"instanceName":"1"}),"instanceName":"1"});
            var Q135;
            Q135=makeQuery(id+"F9.opPattern","COPY",BODY,{"derivedFrom":makeQuery(id+"F7.opPattern","COPY",BODY,{"derivedFrom":makeQuery(id+"F6.opPattern","COPY",BODY,{"derivedFrom":makeQuery(id+"F4.opPattern","COPY",BODY,{"derivedFrom":makeQuery(id+"F1.opRevolve","SWEPT_BODY",BODY,{"disambiguationData":[OSD([sQuery(id+"F0.wireOp",EDGE,"E1")])]}),"instanceName":"1"}),"instanceName":"1"}),"instanceName":"1"}),"instanceName":"1"});
            var Q136;
            Q136=makeQuery(id+"F9.opPattern","COPY",BODY,{"derivedFrom":makeQuery(id+"F7.opPattern","COPY",BODY,{"derivedFrom":makeQuery(id+"F6.opPattern","COPY",BODY,{"derivedFrom":makeQuery(id+"F4.opPattern","COPY",BODY,{"derivedFrom":makeQuery(id+"F2.opPattern","COPY",BODY,{"derivedFrom":makeQuery(id+"F1.opRevolve","SWEPT_BODY",BODY,{"disambiguationData":[OSD([sQuery(id+"F0.wireOp",EDGE,"E1")])]}),"instanceName":"1"}),"instanceName":"1"}),"instanceName":"1"}),"instanceName":"1"}),"instanceName":"1"});
            var Q137;
            Q137=makeQuery(id+"F9.opPattern","COPY",BODY,{"derivedFrom":makeQuery(id+"F7.opPattern","COPY",BODY,{"derivedFrom":makeQuery(id+"F6.opPattern","COPY",BODY,{"derivedFrom":makeQuery(id+"F4.opPattern","COPY",BODY,{"derivedFrom":makeQuery(id+"F3.opPattern","COPY",BODY,{"derivedFrom":makeQuery(id+"F2.opPattern","COPY",BODY,{"derivedFrom":makeQuery(id+"F1.opRevolve","SWEPT_BODY",BODY,{"disambiguationData":[OSD([sQuery(id+"F0.wireOp",EDGE,"E1")])]}),"instanceName":"1"}),"instanceName":"1"}),"instanceName":"1"}),"instanceName":"1"}),"instanceName":"1"}),"instanceName":"1"});
            var Q138;
            Q138=makeQuery(id+"F9.opPattern","COPY",BODY,{"derivedFrom":makeQuery(id+"F7.opPattern","COPY",BODY,{"derivedFrom":makeQuery(id+"F6.opPattern","COPY",BODY,{"derivedFrom":makeQuery(id+"F5.opPattern","COPY",BODY,{"derivedFrom":makeQuery(id+"F1.opRevolve","SWEPT_BODY",BODY,{"disambiguationData":[OSD([sQuery(id+"F0.wireOp",EDGE,"E1")])]}),"instanceName":"1"}),"instanceName":"1"}),"instanceName":"1"}),"instanceName":"1"});
            var Q139;
            Q139=makeQuery(id+"F9.opPattern","COPY",BODY,{"derivedFrom":makeQuery(id+"F7.opPattern","COPY",BODY,{"derivedFrom":makeQuery(id+"F6.opPattern","COPY",BODY,{"derivedFrom":makeQuery(id+"F5.opPattern","COPY",BODY,{"derivedFrom":makeQuery(id+"F2.opPattern","COPY",BODY,{"derivedFrom":makeQuery(id+"F1.opRevolve","SWEPT_BODY",BODY,{"disambiguationData":[OSD([sQuery(id+"F0.wireOp",EDGE,"E1")])]}),"instanceName":"1"}),"instanceName":"1"}),"instanceName":"1"}),"instanceName":"1"}),"instanceName":"1"});
            var Q140;
            Q140=makeQuery(id+"F9.opPattern","COPY",BODY,{"derivedFrom":makeQuery(id+"F7.opPattern","COPY",BODY,{"derivedFrom":makeQuery(id+"F6.opPattern","COPY",BODY,{"derivedFrom":makeQuery(id+"F5.opPattern","COPY",BODY,{"derivedFrom":makeQuery(id+"F3.opPattern","COPY",BODY,{"derivedFrom":makeQuery(id+"F2.opPattern","COPY",BODY,{"derivedFrom":makeQuery(id+"F1.opRevolve","SWEPT_BODY",BODY,{"disambiguationData":[OSD([sQuery(id+"F0.wireOp",EDGE,"E1")])]}),"instanceName":"1"}),"instanceName":"1"}),"instanceName":"1"}),"instanceName":"1"}),"instanceName":"1"}),"instanceName":"1"});
            var Q141;
            Q141=makeQuery(id+"F9.opPattern","COPY",BODY,{"derivedFrom":makeQuery(id+"F7.opPattern","COPY",BODY,{"derivedFrom":makeQuery(id+"F6.opPattern","COPY",BODY,{"derivedFrom":makeQuery(id+"F5.opPattern","COPY",BODY,{"derivedFrom":makeQuery(id+"F4.opPattern","COPY",BODY,{"derivedFrom":makeQuery(id+"F1.opRevolve","SWEPT_BODY",BODY,{"disambiguationData":[OSD([sQuery(id+"F0.wireOp",EDGE,"E1")])]}),"instanceName":"1"}),"instanceName":"1"}),"instanceName":"1"}),"instanceName":"1"}),"instanceName":"1"});
            var Q142;
            Q142=makeQuery(id+"F9.opPattern","COPY",BODY,{"derivedFrom":makeQuery(id+"F7.opPattern","COPY",BODY,{"derivedFrom":makeQuery(id+"F6.opPattern","COPY",BODY,{"derivedFrom":makeQuery(id+"F5.opPattern","COPY",BODY,{"derivedFrom":makeQuery(id+"F4.opPattern","COPY",BODY,{"derivedFrom":makeQuery(id+"F2.opPattern","COPY",BODY,{"derivedFrom":makeQuery(id+"F1.opRevolve","SWEPT_BODY",BODY,{"disambiguationData":[OSD([sQuery(id+"F0.wireOp",EDGE,"E1")])]}),"instanceName":"1"}),"instanceName":"1"}),"instanceName":"1"}),"instanceName":"1"}),"instanceName":"1"}),"instanceName":"1"});
            var Q143;
            Q143=makeQuery(id+"F9.opPattern","COPY",BODY,{"derivedFrom":makeQuery(id+"F7.opPattern","COPY",BODY,{"derivedFrom":makeQuery(id+"F6.opPattern","COPY",BODY,{"derivedFrom":makeQuery(id+"F5.opPattern","COPY",BODY,{"derivedFrom":makeQuery(id+"F4.opPattern","COPY",BODY,{"derivedFrom":makeQuery(id+"F3.opPattern","COPY",BODY,{"derivedFrom":makeQuery(id+"F2.opPattern","COPY",BODY,{"derivedFrom":makeQuery(id+"F1.opRevolve","SWEPT_BODY",BODY,{"disambiguationData":[OSD([sQuery(id+"F0.wireOp",EDGE,"E1")])]}),"instanceName":"1"}),"instanceName":"1"}),"instanceName":"1"}),"instanceName":"1"}),"instanceName":"1"}),"instanceName":"1"}),"instanceName":"1"});
            var Q144;
            Q144=makeQuery(id+"F9.opPattern","COPY",BODY,{"derivedFrom":makeQuery(id+"F8.opPattern","COPY",BODY,{"derivedFrom":makeQuery(id+"F1.opRevolve","SWEPT_BODY",BODY,{"disambiguationData":[OSD([sQuery(id+"F0.wireOp",EDGE,"E1")])]}),"instanceName":"1"}),"instanceName":"1"});
            var Q145;
            Q145=makeQuery(id+"F9.opPattern","COPY",BODY,{"derivedFrom":makeQuery(id+"F8.opPattern","COPY",BODY,{"derivedFrom":makeQuery(id+"F2.opPattern","COPY",BODY,{"derivedFrom":makeQuery(id+"F1.opRevolve","SWEPT_BODY",BODY,{"disambiguationData":[OSD([sQuery(id+"F0.wireOp",EDGE,"E1")])]}),"instanceName":"1"}),"instanceName":"1"}),"instanceName":"1"});
            var Q146;
            Q146=makeQuery(id+"F9.opPattern","COPY",BODY,{"derivedFrom":makeQuery(id+"F8.opPattern","COPY",BODY,{"derivedFrom":makeQuery(id+"F3.opPattern","COPY",BODY,{"derivedFrom":makeQuery(id+"F2.opPattern","COPY",BODY,{"derivedFrom":makeQuery(id+"F1.opRevolve","SWEPT_BODY",BODY,{"disambiguationData":[OSD([sQuery(id+"F0.wireOp",EDGE,"E1")])]}),"instanceName":"1"}),"instanceName":"1"}),"instanceName":"1"}),"instanceName":"1"});
            var Q147;
            Q147=makeQuery(id+"F9.opPattern","COPY",BODY,{"derivedFrom":makeQuery(id+"F8.opPattern","COPY",BODY,{"derivedFrom":makeQuery(id+"F4.opPattern","COPY",BODY,{"derivedFrom":makeQuery(id+"F1.opRevolve","SWEPT_BODY",BODY,{"disambiguationData":[OSD([sQuery(id+"F0.wireOp",EDGE,"E1")])]}),"instanceName":"1"}),"instanceName":"1"}),"instanceName":"1"});
            var Q148;
            Q148=makeQuery(id+"F9.opPattern","COPY",BODY,{"derivedFrom":makeQuery(id+"F8.opPattern","COPY",BODY,{"derivedFrom":makeQuery(id+"F4.opPattern","COPY",BODY,{"derivedFrom":makeQuery(id+"F2.opPattern","COPY",BODY,{"derivedFrom":makeQuery(id+"F1.opRevolve","SWEPT_BODY",BODY,{"disambiguationData":[OSD([sQuery(id+"F0.wireOp",EDGE,"E1")])]}),"instanceName":"1"}),"instanceName":"1"}),"instanceName":"1"}),"instanceName":"1"});
            var Q149;
            Q149=makeQuery(id+"F9.opPattern","COPY",BODY,{"derivedFrom":makeQuery(id+"F8.opPattern","COPY",BODY,{"derivedFrom":makeQuery(id+"F4.opPattern","COPY",BODY,{"derivedFrom":makeQuery(id+"F3.opPattern","COPY",BODY,{"derivedFrom":makeQuery(id+"F2.opPattern","COPY",BODY,{"derivedFrom":makeQuery(id+"F1.opRevolve","SWEPT_BODY",BODY,{"disambiguationData":[OSD([sQuery(id+"F0.wireOp",EDGE,"E1")])]}),"instanceName":"1"}),"instanceName":"1"}),"instanceName":"1"}),"instanceName":"1"}),"instanceName":"1"});
            var Q150;
            Q150=makeQuery(id+"F9.opPattern","COPY",BODY,{"derivedFrom":makeQuery(id+"F8.opPattern","COPY",BODY,{"derivedFrom":makeQuery(id+"F5.opPattern","COPY",BODY,{"derivedFrom":makeQuery(id+"F1.opRevolve","SWEPT_BODY",BODY,{"disambiguationData":[OSD([sQuery(id+"F0.wireOp",EDGE,"E1")])]}),"instanceName":"1"}),"instanceName":"1"}),"instanceName":"1"});
            var Q151;
            Q151=makeQuery(id+"F9.opPattern","COPY",BODY,{"derivedFrom":makeQuery(id+"F8.opPattern","COPY",BODY,{"derivedFrom":makeQuery(id+"F5.opPattern","COPY",BODY,{"derivedFrom":makeQuery(id+"F2.opPattern","COPY",BODY,{"derivedFrom":makeQuery(id+"F1.opRevolve","SWEPT_BODY",BODY,{"disambiguationData":[OSD([sQuery(id+"F0.wireOp",EDGE,"E1")])]}),"instanceName":"1"}),"instanceName":"1"}),"instanceName":"1"}),"instanceName":"1"});
            var Q152;
            Q152=makeQuery(id+"F9.opPattern","COPY",BODY,{"derivedFrom":makeQuery(id+"F8.opPattern","COPY",BODY,{"derivedFrom":makeQuery(id+"F5.opPattern","COPY",BODY,{"derivedFrom":makeQuery(id+"F3.opPattern","COPY",BODY,{"derivedFrom":makeQuery(id+"F2.opPattern","COPY",BODY,{"derivedFrom":makeQuery(id+"F1.opRevolve","SWEPT_BODY",BODY,{"disambiguationData":[OSD([sQuery(id+"F0.wireOp",EDGE,"E1")])]}),"instanceName":"1"}),"instanceName":"1"}),"instanceName":"1"}),"instanceName":"1"}),"instanceName":"1"});
            var Q153;
            Q153=makeQuery(id+"F9.opPattern","COPY",BODY,{"derivedFrom":makeQuery(id+"F8.opPattern","COPY",BODY,{"derivedFrom":makeQuery(id+"F5.opPattern","COPY",BODY,{"derivedFrom":makeQuery(id+"F4.opPattern","COPY",BODY,{"derivedFrom":makeQuery(id+"F1.opRevolve","SWEPT_BODY",BODY,{"disambiguationData":[OSD([sQuery(id+"F0.wireOp",EDGE,"E1")])]}),"instanceName":"1"}),"instanceName":"1"}),"instanceName":"1"}),"instanceName":"1"});
            var Q154;
            Q154=makeQuery(id+"F9.opPattern","COPY",BODY,{"derivedFrom":makeQuery(id+"F8.opPattern","COPY",BODY,{"derivedFrom":makeQuery(id+"F5.opPattern","COPY",BODY,{"derivedFrom":makeQuery(id+"F4.opPattern","COPY",BODY,{"derivedFrom":makeQuery(id+"F2.opPattern","COPY",BODY,{"derivedFrom":makeQuery(id+"F1.opRevolve","SWEPT_BODY",BODY,{"disambiguationData":[OSD([sQuery(id+"F0.wireOp",EDGE,"E1")])]}),"instanceName":"1"}),"instanceName":"1"}),"instanceName":"1"}),"instanceName":"1"}),"instanceName":"1"});
            var Q155;
            Q155=makeQuery(id+"F9.opPattern","COPY",BODY,{"derivedFrom":makeQuery(id+"F8.opPattern","COPY",BODY,{"derivedFrom":makeQuery(id+"F5.opPattern","COPY",BODY,{"derivedFrom":makeQuery(id+"F4.opPattern","COPY",BODY,{"derivedFrom":makeQuery(id+"F3.opPattern","COPY",BODY,{"derivedFrom":makeQuery(id+"F2.opPattern","COPY",BODY,{"derivedFrom":makeQuery(id+"F1.opRevolve","SWEPT_BODY",BODY,{"disambiguationData":[OSD([sQuery(id+"F0.wireOp",EDGE,"E1")])]}),"instanceName":"1"}),"instanceName":"1"}),"instanceName":"1"}),"instanceName":"1"}),"instanceName":"1"}),"instanceName":"1"});
            var Q156;
            Q156=makeQuery(id+"F9.opPattern","COPY",BODY,{"derivedFrom":makeQuery(id+"F8.opPattern","COPY",BODY,{"derivedFrom":makeQuery(id+"F6.opPattern","COPY",BODY,{"derivedFrom":makeQuery(id+"F1.opRevolve","SWEPT_BODY",BODY,{"disambiguationData":[OSD([sQuery(id+"F0.wireOp",EDGE,"E1")])]}),"instanceName":"1"}),"instanceName":"1"}),"instanceName":"1"});
            var Q157;
            Q157=makeQuery(id+"F9.opPattern","COPY",BODY,{"derivedFrom":makeQuery(id+"F8.opPattern","COPY",BODY,{"derivedFrom":makeQuery(id+"F6.opPattern","COPY",BODY,{"derivedFrom":makeQuery(id+"F2.opPattern","COPY",BODY,{"derivedFrom":makeQuery(id+"F1.opRevolve","SWEPT_BODY",BODY,{"disambiguationData":[OSD([sQuery(id+"F0.wireOp",EDGE,"E1")])]}),"instanceName":"1"}),"instanceName":"1"}),"instanceName":"1"}),"instanceName":"1"});
            var Q158;
            Q158=makeQuery(id+"F9.opPattern","COPY",BODY,{"derivedFrom":makeQuery(id+"F8.opPattern","COPY",BODY,{"derivedFrom":makeQuery(id+"F6.opPattern","COPY",BODY,{"derivedFrom":makeQuery(id+"F3.opPattern","COPY",BODY,{"derivedFrom":makeQuery(id+"F2.opPattern","COPY",BODY,{"derivedFrom":makeQuery(id+"F1.opRevolve","SWEPT_BODY",BODY,{"disambiguationData":[OSD([sQuery(id+"F0.wireOp",EDGE,"E1")])]}),"instanceName":"1"}),"instanceName":"1"}),"instanceName":"1"}),"instanceName":"1"}),"instanceName":"1"});
            var Q159;
            Q159=makeQuery(id+"F9.opPattern","COPY",BODY,{"derivedFrom":makeQuery(id+"F8.opPattern","COPY",BODY,{"derivedFrom":makeQuery(id+"F6.opPattern","COPY",BODY,{"derivedFrom":makeQuery(id+"F4.opPattern","COPY",BODY,{"derivedFrom":makeQuery(id+"F1.opRevolve","SWEPT_BODY",BODY,{"disambiguationData":[OSD([sQuery(id+"F0.wireOp",EDGE,"E1")])]}),"instanceName":"1"}),"instanceName":"1"}),"instanceName":"1"}),"instanceName":"1"});
            var Q160;
            Q160=makeQuery(id+"F9.opPattern","COPY",BODY,{"derivedFrom":makeQuery(id+"F8.opPattern","COPY",BODY,{"derivedFrom":makeQuery(id+"F6.opPattern","COPY",BODY,{"derivedFrom":makeQuery(id+"F4.opPattern","COPY",BODY,{"derivedFrom":makeQuery(id+"F2.opPattern","COPY",BODY,{"derivedFrom":makeQuery(id+"F1.opRevolve","SWEPT_BODY",BODY,{"disambiguationData":[OSD([sQuery(id+"F0.wireOp",EDGE,"E1")])]}),"instanceName":"1"}),"instanceName":"1"}),"instanceName":"1"}),"instanceName":"1"}),"instanceName":"1"});
            var Q161;
            Q161=makeQuery(id+"F9.opPattern","COPY",BODY,{"derivedFrom":makeQuery(id+"F8.opPattern","COPY",BODY,{"derivedFrom":makeQuery(id+"F6.opPattern","COPY",BODY,{"derivedFrom":makeQuery(id+"F4.opPattern","COPY",BODY,{"derivedFrom":makeQuery(id+"F3.opPattern","COPY",BODY,{"derivedFrom":makeQuery(id+"F2.opPattern","COPY",BODY,{"derivedFrom":makeQuery(id+"F1.opRevolve","SWEPT_BODY",BODY,{"disambiguationData":[OSD([sQuery(id+"F0.wireOp",EDGE,"E1")])]}),"instanceName":"1"}),"instanceName":"1"}),"instanceName":"1"}),"instanceName":"1"}),"instanceName":"1"}),"instanceName":"1"});
            var Q162;
            Q162=makeQuery(id+"F9.opPattern","COPY",BODY,{"derivedFrom":makeQuery(id+"F8.opPattern","COPY",BODY,{"derivedFrom":makeQuery(id+"F6.opPattern","COPY",BODY,{"derivedFrom":makeQuery(id+"F5.opPattern","COPY",BODY,{"derivedFrom":makeQuery(id+"F1.opRevolve","SWEPT_BODY",BODY,{"disambiguationData":[OSD([sQuery(id+"F0.wireOp",EDGE,"E1")])]}),"instanceName":"1"}),"instanceName":"1"}),"instanceName":"1"}),"instanceName":"1"});
            var Q163;
            Q163=makeQuery(id+"F9.opPattern","COPY",BODY,{"derivedFrom":makeQuery(id+"F8.opPattern","COPY",BODY,{"derivedFrom":makeQuery(id+"F6.opPattern","COPY",BODY,{"derivedFrom":makeQuery(id+"F5.opPattern","COPY",BODY,{"derivedFrom":makeQuery(id+"F2.opPattern","COPY",BODY,{"derivedFrom":makeQuery(id+"F1.opRevolve","SWEPT_BODY",BODY,{"disambiguationData":[OSD([sQuery(id+"F0.wireOp",EDGE,"E1")])]}),"instanceName":"1"}),"instanceName":"1"}),"instanceName":"1"}),"instanceName":"1"}),"instanceName":"1"});
            var Q164;
            Q164=makeQuery(id+"F9.opPattern","COPY",BODY,{"derivedFrom":makeQuery(id+"F8.opPattern","COPY",BODY,{"derivedFrom":makeQuery(id+"F6.opPattern","COPY",BODY,{"derivedFrom":makeQuery(id+"F5.opPattern","COPY",BODY,{"derivedFrom":makeQuery(id+"F3.opPattern","COPY",BODY,{"derivedFrom":makeQuery(id+"F2.opPattern","COPY",BODY,{"derivedFrom":makeQuery(id+"F1.opRevolve","SWEPT_BODY",BODY,{"disambiguationData":[OSD([sQuery(id+"F0.wireOp",EDGE,"E1")])]}),"instanceName":"1"}),"instanceName":"1"}),"instanceName":"1"}),"instanceName":"1"}),"instanceName":"1"}),"instanceName":"1"});
            var Q165;
            Q165=makeQuery(id+"F9.opPattern","COPY",BODY,{"derivedFrom":makeQuery(id+"F8.opPattern","COPY",BODY,{"derivedFrom":makeQuery(id+"F6.opPattern","COPY",BODY,{"derivedFrom":makeQuery(id+"F5.opPattern","COPY",BODY,{"derivedFrom":makeQuery(id+"F4.opPattern","COPY",BODY,{"derivedFrom":makeQuery(id+"F1.opRevolve","SWEPT_BODY",BODY,{"disambiguationData":[OSD([sQuery(id+"F0.wireOp",EDGE,"E1")])]}),"instanceName":"1"}),"instanceName":"1"}),"instanceName":"1"}),"instanceName":"1"}),"instanceName":"1"});
            var Q166;
            Q166=makeQuery(id+"F9.opPattern","COPY",BODY,{"derivedFrom":makeQuery(id+"F8.opPattern","COPY",BODY,{"derivedFrom":makeQuery(id+"F6.opPattern","COPY",BODY,{"derivedFrom":makeQuery(id+"F5.opPattern","COPY",BODY,{"derivedFrom":makeQuery(id+"F4.opPattern","COPY",BODY,{"derivedFrom":makeQuery(id+"F2.opPattern","COPY",BODY,{"derivedFrom":makeQuery(id+"F1.opRevolve","SWEPT_BODY",BODY,{"disambiguationData":[OSD([sQuery(id+"F0.wireOp",EDGE,"E1")])]}),"instanceName":"1"}),"instanceName":"1"}),"instanceName":"1"}),"instanceName":"1"}),"instanceName":"1"}),"instanceName":"1"});
            var Q167;
            Q167=makeQuery(id+"F9.opPattern","COPY",BODY,{"derivedFrom":makeQuery(id+"F8.opPattern","COPY",BODY,{"derivedFrom":makeQuery(id+"F6.opPattern","COPY",BODY,{"derivedFrom":makeQuery(id+"F5.opPattern","COPY",BODY,{"derivedFrom":makeQuery(id+"F4.opPattern","COPY",BODY,{"derivedFrom":makeQuery(id+"F3.opPattern","COPY",BODY,{"derivedFrom":makeQuery(id+"F2.opPattern","COPY",BODY,{"derivedFrom":makeQuery(id+"F1.opRevolve","SWEPT_BODY",BODY,{"disambiguationData":[OSD([sQuery(id+"F0.wireOp",EDGE,"E1")])]}),"instanceName":"1"}),"instanceName":"1"}),"instanceName":"1"}),"instanceName":"1"}),"instanceName":"1"}),"instanceName":"1"}),"instanceName":"1"});
            var Q168;
            Q168=makeQuery(id+"F9.opPattern","COPY",BODY,{"derivedFrom":makeQuery(id+"F8.opPattern","COPY",BODY,{"derivedFrom":makeQuery(id+"F7.opPattern","COPY",BODY,{"derivedFrom":makeQuery(id+"F1.opRevolve","SWEPT_BODY",BODY,{"disambiguationData":[OSD([sQuery(id+"F0.wireOp",EDGE,"E1")])]}),"instanceName":"1"}),"instanceName":"1"}),"instanceName":"1"});
            var Q169;
            Q169=makeQuery(id+"F9.opPattern","COPY",BODY,{"derivedFrom":makeQuery(id+"F8.opPattern","COPY",BODY,{"derivedFrom":makeQuery(id+"F7.opPattern","COPY",BODY,{"derivedFrom":makeQuery(id+"F2.opPattern","COPY",BODY,{"derivedFrom":makeQuery(id+"F1.opRevolve","SWEPT_BODY",BODY,{"disambiguationData":[OSD([sQuery(id+"F0.wireOp",EDGE,"E1")])]}),"instanceName":"1"}),"instanceName":"1"}),"instanceName":"1"}),"instanceName":"1"});
            var Q170;
            Q170=makeQuery(id+"F9.opPattern","COPY",BODY,{"derivedFrom":makeQuery(id+"F8.opPattern","COPY",BODY,{"derivedFrom":makeQuery(id+"F7.opPattern","COPY",BODY,{"derivedFrom":makeQuery(id+"F3.opPattern","COPY",BODY,{"derivedFrom":makeQuery(id+"F2.opPattern","COPY",BODY,{"derivedFrom":makeQuery(id+"F1.opRevolve","SWEPT_BODY",BODY,{"disambiguationData":[OSD([sQuery(id+"F0.wireOp",EDGE,"E1")])]}),"instanceName":"1"}),"instanceName":"1"}),"instanceName":"1"}),"instanceName":"1"}),"instanceName":"1"});
            var Q171;
            Q171=makeQuery(id+"F9.opPattern","COPY",BODY,{"derivedFrom":makeQuery(id+"F8.opPattern","COPY",BODY,{"derivedFrom":makeQuery(id+"F7.opPattern","COPY",BODY,{"derivedFrom":makeQuery(id+"F4.opPattern","COPY",BODY,{"derivedFrom":makeQuery(id+"F1.opRevolve","SWEPT_BODY",BODY,{"disambiguationData":[OSD([sQuery(id+"F0.wireOp",EDGE,"E1")])]}),"instanceName":"1"}),"instanceName":"1"}),"instanceName":"1"}),"instanceName":"1"});
            var Q172;
            Q172=makeQuery(id+"F9.opPattern","COPY",BODY,{"derivedFrom":makeQuery(id+"F8.opPattern","COPY",BODY,{"derivedFrom":makeQuery(id+"F7.opPattern","COPY",BODY,{"derivedFrom":makeQuery(id+"F4.opPattern","COPY",BODY,{"derivedFrom":makeQuery(id+"F2.opPattern","COPY",BODY,{"derivedFrom":makeQuery(id+"F1.opRevolve","SWEPT_BODY",BODY,{"disambiguationData":[OSD([sQuery(id+"F0.wireOp",EDGE,"E1")])]}),"instanceName":"1"}),"instanceName":"1"}),"instanceName":"1"}),"instanceName":"1"}),"instanceName":"1"});
            var Q173;
            Q173=makeQuery(id+"F9.opPattern","COPY",BODY,{"derivedFrom":makeQuery(id+"F8.opPattern","COPY",BODY,{"derivedFrom":makeQuery(id+"F7.opPattern","COPY",BODY,{"derivedFrom":makeQuery(id+"F4.opPattern","COPY",BODY,{"derivedFrom":makeQuery(id+"F3.opPattern","COPY",BODY,{"derivedFrom":makeQuery(id+"F2.opPattern","COPY",BODY,{"derivedFrom":makeQuery(id+"F1.opRevolve","SWEPT_BODY",BODY,{"disambiguationData":[OSD([sQuery(id+"F0.wireOp",EDGE,"E1")])]}),"instanceName":"1"}),"instanceName":"1"}),"instanceName":"1"}),"instanceName":"1"}),"instanceName":"1"}),"instanceName":"1"});
            var Q174;
            Q174=makeQuery(id+"F9.opPattern","COPY",BODY,{"derivedFrom":makeQuery(id+"F8.opPattern","COPY",BODY,{"derivedFrom":makeQuery(id+"F7.opPattern","COPY",BODY,{"derivedFrom":makeQuery(id+"F5.opPattern","COPY",BODY,{"derivedFrom":makeQuery(id+"F1.opRevolve","SWEPT_BODY",BODY,{"disambiguationData":[OSD([sQuery(id+"F0.wireOp",EDGE,"E1")])]}),"instanceName":"1"}),"instanceName":"1"}),"instanceName":"1"}),"instanceName":"1"});
            var Q175;
            Q175=makeQuery(id+"F9.opPattern","COPY",BODY,{"derivedFrom":makeQuery(id+"F8.opPattern","COPY",BODY,{"derivedFrom":makeQuery(id+"F7.opPattern","COPY",BODY,{"derivedFrom":makeQuery(id+"F5.opPattern","COPY",BODY,{"derivedFrom":makeQuery(id+"F2.opPattern","COPY",BODY,{"derivedFrom":makeQuery(id+"F1.opRevolve","SWEPT_BODY",BODY,{"disambiguationData":[OSD([sQuery(id+"F0.wireOp",EDGE,"E1")])]}),"instanceName":"1"}),"instanceName":"1"}),"instanceName":"1"}),"instanceName":"1"}),"instanceName":"1"});
            var Q176;
            Q176=makeQuery(id+"F9.opPattern","COPY",BODY,{"derivedFrom":makeQuery(id+"F8.opPattern","COPY",BODY,{"derivedFrom":makeQuery(id+"F7.opPattern","COPY",BODY,{"derivedFrom":makeQuery(id+"F5.opPattern","COPY",BODY,{"derivedFrom":makeQuery(id+"F3.opPattern","COPY",BODY,{"derivedFrom":makeQuery(id+"F2.opPattern","COPY",BODY,{"derivedFrom":makeQuery(id+"F1.opRevolve","SWEPT_BODY",BODY,{"disambiguationData":[OSD([sQuery(id+"F0.wireOp",EDGE,"E1")])]}),"instanceName":"1"}),"instanceName":"1"}),"instanceName":"1"}),"instanceName":"1"}),"instanceName":"1"}),"instanceName":"1"});
            var Q177;
            Q177=makeQuery(id+"F9.opPattern","COPY",BODY,{"derivedFrom":makeQuery(id+"F8.opPattern","COPY",BODY,{"derivedFrom":makeQuery(id+"F7.opPattern","COPY",BODY,{"derivedFrom":makeQuery(id+"F5.opPattern","COPY",BODY,{"derivedFrom":makeQuery(id+"F4.opPattern","COPY",BODY,{"derivedFrom":makeQuery(id+"F1.opRevolve","SWEPT_BODY",BODY,{"disambiguationData":[OSD([sQuery(id+"F0.wireOp",EDGE,"E1")])]}),"instanceName":"1"}),"instanceName":"1"}),"instanceName":"1"}),"instanceName":"1"}),"instanceName":"1"});
            var Q178;
            Q178=makeQuery(id+"F9.opPattern","COPY",BODY,{"derivedFrom":makeQuery(id+"F8.opPattern","COPY",BODY,{"derivedFrom":makeQuery(id+"F7.opPattern","COPY",BODY,{"derivedFrom":makeQuery(id+"F5.opPattern","COPY",BODY,{"derivedFrom":makeQuery(id+"F4.opPattern","COPY",BODY,{"derivedFrom":makeQuery(id+"F2.opPattern","COPY",BODY,{"derivedFrom":makeQuery(id+"F1.opRevolve","SWEPT_BODY",BODY,{"disambiguationData":[OSD([sQuery(id+"F0.wireOp",EDGE,"E1")])]}),"instanceName":"1"}),"instanceName":"1"}),"instanceName":"1"}),"instanceName":"1"}),"instanceName":"1"}),"instanceName":"1"});
            var Q179;
            Q179=makeQuery(id+"F9.opPattern","COPY",BODY,{"derivedFrom":makeQuery(id+"F8.opPattern","COPY",BODY,{"derivedFrom":makeQuery(id+"F7.opPattern","COPY",BODY,{"derivedFrom":makeQuery(id+"F5.opPattern","COPY",BODY,{"derivedFrom":makeQuery(id+"F4.opPattern","COPY",BODY,{"derivedFrom":makeQuery(id+"F3.opPattern","COPY",BODY,{"derivedFrom":makeQuery(id+"F2.opPattern","COPY",BODY,{"derivedFrom":makeQuery(id+"F1.opRevolve","SWEPT_BODY",BODY,{"disambiguationData":[OSD([sQuery(id+"F0.wireOp",EDGE,"E1")])]}),"instanceName":"1"}),"instanceName":"1"}),"instanceName":"1"}),"instanceName":"1"}),"instanceName":"1"}),"instanceName":"1"}),"instanceName":"1"});
            var Q180;
            Q180=makeQuery(id+"F9.opPattern","COPY",BODY,{"derivedFrom":makeQuery(id+"F8.opPattern","COPY",BODY,{"derivedFrom":makeQuery(id+"F7.opPattern","COPY",BODY,{"derivedFrom":makeQuery(id+"F6.opPattern","COPY",BODY,{"derivedFrom":makeQuery(id+"F1.opRevolve","SWEPT_BODY",BODY,{"disambiguationData":[OSD([sQuery(id+"F0.wireOp",EDGE,"E1")])]}),"instanceName":"1"}),"instanceName":"1"}),"instanceName":"1"}),"instanceName":"1"});
            var Q181;
            Q181=makeQuery(id+"F9.opPattern","COPY",BODY,{"derivedFrom":makeQuery(id+"F8.opPattern","COPY",BODY,{"derivedFrom":makeQuery(id+"F7.opPattern","COPY",BODY,{"derivedFrom":makeQuery(id+"F6.opPattern","COPY",BODY,{"derivedFrom":makeQuery(id+"F2.opPattern","COPY",BODY,{"derivedFrom":makeQuery(id+"F1.opRevolve","SWEPT_BODY",BODY,{"disambiguationData":[OSD([sQuery(id+"F0.wireOp",EDGE,"E1")])]}),"instanceName":"1"}),"instanceName":"1"}),"instanceName":"1"}),"instanceName":"1"}),"instanceName":"1"});
            var Q182;
            Q182=makeQuery(id+"F9.opPattern","COPY",BODY,{"derivedFrom":makeQuery(id+"F8.opPattern","COPY",BODY,{"derivedFrom":makeQuery(id+"F7.opPattern","COPY",BODY,{"derivedFrom":makeQuery(id+"F6.opPattern","COPY",BODY,{"derivedFrom":makeQuery(id+"F3.opPattern","COPY",BODY,{"derivedFrom":makeQuery(id+"F2.opPattern","COPY",BODY,{"derivedFrom":makeQuery(id+"F1.opRevolve","SWEPT_BODY",BODY,{"disambiguationData":[OSD([sQuery(id+"F0.wireOp",EDGE,"E1")])]}),"instanceName":"1"}),"instanceName":"1"}),"instanceName":"1"}),"instanceName":"1"}),"instanceName":"1"}),"instanceName":"1"});
            var Q183;
            Q183=makeQuery(id+"F9.opPattern","COPY",BODY,{"derivedFrom":makeQuery(id+"F8.opPattern","COPY",BODY,{"derivedFrom":makeQuery(id+"F7.opPattern","COPY",BODY,{"derivedFrom":makeQuery(id+"F6.opPattern","COPY",BODY,{"derivedFrom":makeQuery(id+"F4.opPattern","COPY",BODY,{"derivedFrom":makeQuery(id+"F1.opRevolve","SWEPT_BODY",BODY,{"disambiguationData":[OSD([sQuery(id+"F0.wireOp",EDGE,"E1")])]}),"instanceName":"1"}),"instanceName":"1"}),"instanceName":"1"}),"instanceName":"1"}),"instanceName":"1"});
            var Q184;
            Q184=makeQuery(id+"F9.opPattern","COPY",BODY,{"derivedFrom":makeQuery(id+"F8.opPattern","COPY",BODY,{"derivedFrom":makeQuery(id+"F7.opPattern","COPY",BODY,{"derivedFrom":makeQuery(id+"F6.opPattern","COPY",BODY,{"derivedFrom":makeQuery(id+"F4.opPattern","COPY",BODY,{"derivedFrom":makeQuery(id+"F2.opPattern","COPY",BODY,{"derivedFrom":makeQuery(id+"F1.opRevolve","SWEPT_BODY",BODY,{"disambiguationData":[OSD([sQuery(id+"F0.wireOp",EDGE,"E1")])]}),"instanceName":"1"}),"instanceName":"1"}),"instanceName":"1"}),"instanceName":"1"}),"instanceName":"1"}),"instanceName":"1"});
            var Q185;
            Q185=makeQuery(id+"F9.opPattern","COPY",BODY,{"derivedFrom":makeQuery(id+"F8.opPattern","COPY",BODY,{"derivedFrom":makeQuery(id+"F7.opPattern","COPY",BODY,{"derivedFrom":makeQuery(id+"F6.opPattern","COPY",BODY,{"derivedFrom":makeQuery(id+"F4.opPattern","COPY",BODY,{"derivedFrom":makeQuery(id+"F3.opPattern","COPY",BODY,{"derivedFrom":makeQuery(id+"F2.opPattern","COPY",BODY,{"derivedFrom":makeQuery(id+"F1.opRevolve","SWEPT_BODY",BODY,{"disambiguationData":[OSD([sQuery(id+"F0.wireOp",EDGE,"E1")])]}),"instanceName":"1"}),"instanceName":"1"}),"instanceName":"1"}),"instanceName":"1"}),"instanceName":"1"}),"instanceName":"1"}),"instanceName":"1"});
            var Q186;
            Q186=makeQuery(id+"F9.opPattern","COPY",BODY,{"derivedFrom":makeQuery(id+"F8.opPattern","COPY",BODY,{"derivedFrom":makeQuery(id+"F7.opPattern","COPY",BODY,{"derivedFrom":makeQuery(id+"F6.opPattern","COPY",BODY,{"derivedFrom":makeQuery(id+"F5.opPattern","COPY",BODY,{"derivedFrom":makeQuery(id+"F1.opRevolve","SWEPT_BODY",BODY,{"disambiguationData":[OSD([sQuery(id+"F0.wireOp",EDGE,"E1")])]}),"instanceName":"1"}),"instanceName":"1"}),"instanceName":"1"}),"instanceName":"1"}),"instanceName":"1"});
            var Q187;
            Q187=makeQuery(id+"F9.opPattern","COPY",BODY,{"derivedFrom":makeQuery(id+"F8.opPattern","COPY",BODY,{"derivedFrom":makeQuery(id+"F7.opPattern","COPY",BODY,{"derivedFrom":makeQuery(id+"F6.opPattern","COPY",BODY,{"derivedFrom":makeQuery(id+"F5.opPattern","COPY",BODY,{"derivedFrom":makeQuery(id+"F2.opPattern","COPY",BODY,{"derivedFrom":makeQuery(id+"F1.opRevolve","SWEPT_BODY",BODY,{"disambiguationData":[OSD([sQuery(id+"F0.wireOp",EDGE,"E1")])]}),"instanceName":"1"}),"instanceName":"1"}),"instanceName":"1"}),"instanceName":"1"}),"instanceName":"1"}),"instanceName":"1"});
            var Q188;
            Q188=makeQuery(id+"F9.opPattern","COPY",BODY,{"derivedFrom":makeQuery(id+"F8.opPattern","COPY",BODY,{"derivedFrom":makeQuery(id+"F7.opPattern","COPY",BODY,{"derivedFrom":makeQuery(id+"F6.opPattern","COPY",BODY,{"derivedFrom":makeQuery(id+"F5.opPattern","COPY",BODY,{"derivedFrom":makeQuery(id+"F3.opPattern","COPY",BODY,{"derivedFrom":makeQuery(id+"F2.opPattern","COPY",BODY,{"derivedFrom":makeQuery(id+"F1.opRevolve","SWEPT_BODY",BODY,{"disambiguationData":[OSD([sQuery(id+"F0.wireOp",EDGE,"E1")])]}),"instanceName":"1"}),"instanceName":"1"}),"instanceName":"1"}),"instanceName":"1"}),"instanceName":"1"}),"instanceName":"1"}),"instanceName":"1"});
            var Q189;
            Q189=makeQuery(id+"F9.opPattern","COPY",BODY,{"derivedFrom":makeQuery(id+"F8.opPattern","COPY",BODY,{"derivedFrom":makeQuery(id+"F7.opPattern","COPY",BODY,{"derivedFrom":makeQuery(id+"F6.opPattern","COPY",BODY,{"derivedFrom":makeQuery(id+"F5.opPattern","COPY",BODY,{"derivedFrom":makeQuery(id+"F4.opPattern","COPY",BODY,{"derivedFrom":makeQuery(id+"F1.opRevolve","SWEPT_BODY",BODY,{"disambiguationData":[OSD([sQuery(id+"F0.wireOp",EDGE,"E1")])]}),"instanceName":"1"}),"instanceName":"1"}),"instanceName":"1"}),"instanceName":"1"}),"instanceName":"1"}),"instanceName":"1"});
            var Q190;
            Q190=makeQuery(id+"F9.opPattern","COPY",BODY,{"derivedFrom":makeQuery(id+"F8.opPattern","COPY",BODY,{"derivedFrom":makeQuery(id+"F7.opPattern","COPY",BODY,{"derivedFrom":makeQuery(id+"F6.opPattern","COPY",BODY,{"derivedFrom":makeQuery(id+"F5.opPattern","COPY",BODY,{"derivedFrom":makeQuery(id+"F4.opPattern","COPY",BODY,{"derivedFrom":makeQuery(id+"F2.opPattern","COPY",BODY,{"derivedFrom":makeQuery(id+"F1.opRevolve","SWEPT_BODY",BODY,{"disambiguationData":[OSD([sQuery(id+"F0.wireOp",EDGE,"E1")])]}),"instanceName":"1"}),"instanceName":"1"}),"instanceName":"1"}),"instanceName":"1"}),"instanceName":"1"}),"instanceName":"1"}),"instanceName":"1"});
            var Q191;
            Q191=makeQuery(id+"F9.opPattern","COPY",BODY,{"derivedFrom":makeQuery(id+"F8.opPattern","COPY",BODY,{"derivedFrom":makeQuery(id+"F7.opPattern","COPY",BODY,{"derivedFrom":makeQuery(id+"F6.opPattern","COPY",BODY,{"derivedFrom":makeQuery(id+"F5.opPattern","COPY",BODY,{"derivedFrom":makeQuery(id+"F4.opPattern","COPY",BODY,{"derivedFrom":makeQuery(id+"F3.opPattern","COPY",BODY,{"derivedFrom":makeQuery(id+"F2.opPattern","COPY",BODY,{"derivedFrom":makeQuery(id+"F1.opRevolve","SWEPT_BODY",BODY,{"disambiguationData":[OSD([sQuery(id+"F0.wireOp",EDGE,"E1")])]}),"instanceName":"1"}),"instanceName":"1"}),"instanceName":"1"}),"instanceName":"1"}),"instanceName":"1"}),"instanceName":"1"}),"instanceName":"1"}),"instanceName":"1"});
            var Q192;
            Q192=makeQuery(id+"F10.opPattern","COPY",BODY,{"derivedFrom":makeQuery(id+"F1.opRevolve","SWEPT_BODY",BODY,{"disambiguationData":[OSD([sQuery(id+"F0.wireOp",EDGE,"E1")])]}),"instanceName":"1"});
            var Q193;
            Q193=makeQuery(id+"F10.opPattern","COPY",BODY,{"derivedFrom":makeQuery(id+"F2.opPattern","COPY",BODY,{"derivedFrom":makeQuery(id+"F1.opRevolve","SWEPT_BODY",BODY,{"disambiguationData":[OSD([sQuery(id+"F0.wireOp",EDGE,"E1")])]}),"instanceName":"1"}),"instanceName":"1"});
            var Q194;
            Q194=makeQuery(id+"F10.opPattern","COPY",BODY,{"derivedFrom":makeQuery(id+"F3.opPattern","COPY",BODY,{"derivedFrom":makeQuery(id+"F2.opPattern","COPY",BODY,{"derivedFrom":makeQuery(id+"F1.opRevolve","SWEPT_BODY",BODY,{"disambiguationData":[OSD([sQuery(id+"F0.wireOp",EDGE,"E1")])]}),"instanceName":"1"}),"instanceName":"1"}),"instanceName":"1"});
            var Q195;
            Q195=makeQuery(id+"F10.opPattern","COPY",BODY,{"derivedFrom":makeQuery(id+"F4.opPattern","COPY",BODY,{"derivedFrom":makeQuery(id+"F1.opRevolve","SWEPT_BODY",BODY,{"disambiguationData":[OSD([sQuery(id+"F0.wireOp",EDGE,"E1")])]}),"instanceName":"1"}),"instanceName":"1"});
            var Q196;
            Q196=makeQuery(id+"F10.opPattern","COPY",BODY,{"derivedFrom":makeQuery(id+"F4.opPattern","COPY",BODY,{"derivedFrom":makeQuery(id+"F2.opPattern","COPY",BODY,{"derivedFrom":makeQuery(id+"F1.opRevolve","SWEPT_BODY",BODY,{"disambiguationData":[OSD([sQuery(id+"F0.wireOp",EDGE,"E1")])]}),"instanceName":"1"}),"instanceName":"1"}),"instanceName":"1"});
            var Q197;
            Q197=makeQuery(id+"F10.opPattern","COPY",BODY,{"derivedFrom":makeQuery(id+"F4.opPattern","COPY",BODY,{"derivedFrom":makeQuery(id+"F3.opPattern","COPY",BODY,{"derivedFrom":makeQuery(id+"F2.opPattern","COPY",BODY,{"derivedFrom":makeQuery(id+"F1.opRevolve","SWEPT_BODY",BODY,{"disambiguationData":[OSD([sQuery(id+"F0.wireOp",EDGE,"E1")])]}),"instanceName":"1"}),"instanceName":"1"}),"instanceName":"1"}),"instanceName":"1"});
            var Q198;
            Q198=makeQuery(id+"F10.opPattern","COPY",BODY,{"derivedFrom":makeQuery(id+"F5.opPattern","COPY",BODY,{"derivedFrom":makeQuery(id+"F1.opRevolve","SWEPT_BODY",BODY,{"disambiguationData":[OSD([sQuery(id+"F0.wireOp",EDGE,"E1")])]}),"instanceName":"1"}),"instanceName":"1"});
            var Q199;
            Q199=makeQuery(id+"F10.opPattern","COPY",BODY,{"derivedFrom":makeQuery(id+"F5.opPattern","COPY",BODY,{"derivedFrom":makeQuery(id+"F2.opPattern","COPY",BODY,{"derivedFrom":makeQuery(id+"F1.opRevolve","SWEPT_BODY",BODY,{"disambiguationData":[OSD([sQuery(id+"F0.wireOp",EDGE,"E1")])]}),"instanceName":"1"}),"instanceName":"1"}),"instanceName":"1"});
            var Q200;
            Q200=makeQuery(id+"F10.opPattern","COPY",BODY,{"derivedFrom":makeQuery(id+"F5.opPattern","COPY",BODY,{"derivedFrom":makeQuery(id+"F3.opPattern","COPY",BODY,{"derivedFrom":makeQuery(id+"F2.opPattern","COPY",BODY,{"derivedFrom":makeQuery(id+"F1.opRevolve","SWEPT_BODY",BODY,{"disambiguationData":[OSD([sQuery(id+"F0.wireOp",EDGE,"E1")])]}),"instanceName":"1"}),"instanceName":"1"}),"instanceName":"1"}),"instanceName":"1"});
            var Q201;
            Q201=makeQuery(id+"F10.opPattern","COPY",BODY,{"derivedFrom":makeQuery(id+"F5.opPattern","COPY",BODY,{"derivedFrom":makeQuery(id+"F4.opPattern","COPY",BODY,{"derivedFrom":makeQuery(id+"F1.opRevolve","SWEPT_BODY",BODY,{"disambiguationData":[OSD([sQuery(id+"F0.wireOp",EDGE,"E1")])]}),"instanceName":"1"}),"instanceName":"1"}),"instanceName":"1"});
            var Q202;
            Q202=makeQuery(id+"F10.opPattern","COPY",BODY,{"derivedFrom":makeQuery(id+"F5.opPattern","COPY",BODY,{"derivedFrom":makeQuery(id+"F4.opPattern","COPY",BODY,{"derivedFrom":makeQuery(id+"F2.opPattern","COPY",BODY,{"derivedFrom":makeQuery(id+"F1.opRevolve","SWEPT_BODY",BODY,{"disambiguationData":[OSD([sQuery(id+"F0.wireOp",EDGE,"E1")])]}),"instanceName":"1"}),"instanceName":"1"}),"instanceName":"1"}),"instanceName":"1"});
            var Q203;
            Q203=makeQuery(id+"F10.opPattern","COPY",BODY,{"derivedFrom":makeQuery(id+"F5.opPattern","COPY",BODY,{"derivedFrom":makeQuery(id+"F4.opPattern","COPY",BODY,{"derivedFrom":makeQuery(id+"F3.opPattern","COPY",BODY,{"derivedFrom":makeQuery(id+"F2.opPattern","COPY",BODY,{"derivedFrom":makeQuery(id+"F1.opRevolve","SWEPT_BODY",BODY,{"disambiguationData":[OSD([sQuery(id+"F0.wireOp",EDGE,"E1")])]}),"instanceName":"1"}),"instanceName":"1"}),"instanceName":"1"}),"instanceName":"1"}),"instanceName":"1"});
            var Q204;
            Q204=makeQuery(id+"F10.opPattern","COPY",BODY,{"derivedFrom":makeQuery(id+"F6.opPattern","COPY",BODY,{"derivedFrom":makeQuery(id+"F1.opRevolve","SWEPT_BODY",BODY,{"disambiguationData":[OSD([sQuery(id+"F0.wireOp",EDGE,"E1")])]}),"instanceName":"1"}),"instanceName":"1"});
            var Q205;
            Q205=makeQuery(id+"F10.opPattern","COPY",BODY,{"derivedFrom":makeQuery(id+"F6.opPattern","COPY",BODY,{"derivedFrom":makeQuery(id+"F2.opPattern","COPY",BODY,{"derivedFrom":makeQuery(id+"F1.opRevolve","SWEPT_BODY",BODY,{"disambiguationData":[OSD([sQuery(id+"F0.wireOp",EDGE,"E1")])]}),"instanceName":"1"}),"instanceName":"1"}),"instanceName":"1"});
            var Q206;
            Q206=makeQuery(id+"F10.opPattern","COPY",BODY,{"derivedFrom":makeQuery(id+"F6.opPattern","COPY",BODY,{"derivedFrom":makeQuery(id+"F3.opPattern","COPY",BODY,{"derivedFrom":makeQuery(id+"F2.opPattern","COPY",BODY,{"derivedFrom":makeQuery(id+"F1.opRevolve","SWEPT_BODY",BODY,{"disambiguationData":[OSD([sQuery(id+"F0.wireOp",EDGE,"E1")])]}),"instanceName":"1"}),"instanceName":"1"}),"instanceName":"1"}),"instanceName":"1"});
            var Q207;
            Q207=makeQuery(id+"F10.opPattern","COPY",BODY,{"derivedFrom":makeQuery(id+"F6.opPattern","COPY",BODY,{"derivedFrom":makeQuery(id+"F4.opPattern","COPY",BODY,{"derivedFrom":makeQuery(id+"F1.opRevolve","SWEPT_BODY",BODY,{"disambiguationData":[OSD([sQuery(id+"F0.wireOp",EDGE,"E1")])]}),"instanceName":"1"}),"instanceName":"1"}),"instanceName":"1"});
            var Q208;
            Q208=makeQuery(id+"F10.opPattern","COPY",BODY,{"derivedFrom":makeQuery(id+"F6.opPattern","COPY",BODY,{"derivedFrom":makeQuery(id+"F4.opPattern","COPY",BODY,{"derivedFrom":makeQuery(id+"F2.opPattern","COPY",BODY,{"derivedFrom":makeQuery(id+"F1.opRevolve","SWEPT_BODY",BODY,{"disambiguationData":[OSD([sQuery(id+"F0.wireOp",EDGE,"E1")])]}),"instanceName":"1"}),"instanceName":"1"}),"instanceName":"1"}),"instanceName":"1"});
            var Q209;
            Q209=makeQuery(id+"F10.opPattern","COPY",BODY,{"derivedFrom":makeQuery(id+"F6.opPattern","COPY",BODY,{"derivedFrom":makeQuery(id+"F4.opPattern","COPY",BODY,{"derivedFrom":makeQuery(id+"F3.opPattern","COPY",BODY,{"derivedFrom":makeQuery(id+"F2.opPattern","COPY",BODY,{"derivedFrom":makeQuery(id+"F1.opRevolve","SWEPT_BODY",BODY,{"disambiguationData":[OSD([sQuery(id+"F0.wireOp",EDGE,"E1")])]}),"instanceName":"1"}),"instanceName":"1"}),"instanceName":"1"}),"instanceName":"1"}),"instanceName":"1"});
            var Q210;
            Q210=makeQuery(id+"F10.opPattern","COPY",BODY,{"derivedFrom":makeQuery(id+"F6.opPattern","COPY",BODY,{"derivedFrom":makeQuery(id+"F5.opPattern","COPY",BODY,{"derivedFrom":makeQuery(id+"F1.opRevolve","SWEPT_BODY",BODY,{"disambiguationData":[OSD([sQuery(id+"F0.wireOp",EDGE,"E1")])]}),"instanceName":"1"}),"instanceName":"1"}),"instanceName":"1"});
            var Q211;
            Q211=makeQuery(id+"F10.opPattern","COPY",BODY,{"derivedFrom":makeQuery(id+"F6.opPattern","COPY",BODY,{"derivedFrom":makeQuery(id+"F5.opPattern","COPY",BODY,{"derivedFrom":makeQuery(id+"F2.opPattern","COPY",BODY,{"derivedFrom":makeQuery(id+"F1.opRevolve","SWEPT_BODY",BODY,{"disambiguationData":[OSD([sQuery(id+"F0.wireOp",EDGE,"E1")])]}),"instanceName":"1"}),"instanceName":"1"}),"instanceName":"1"}),"instanceName":"1"});
            var Q212;
            Q212=makeQuery(id+"F10.opPattern","COPY",BODY,{"derivedFrom":makeQuery(id+"F6.opPattern","COPY",BODY,{"derivedFrom":makeQuery(id+"F5.opPattern","COPY",BODY,{"derivedFrom":makeQuery(id+"F3.opPattern","COPY",BODY,{"derivedFrom":makeQuery(id+"F2.opPattern","COPY",BODY,{"derivedFrom":makeQuery(id+"F1.opRevolve","SWEPT_BODY",BODY,{"disambiguationData":[OSD([sQuery(id+"F0.wireOp",EDGE,"E1")])]}),"instanceName":"1"}),"instanceName":"1"}),"instanceName":"1"}),"instanceName":"1"}),"instanceName":"1"});
            var Q213;
            Q213=makeQuery(id+"F10.opPattern","COPY",BODY,{"derivedFrom":makeQuery(id+"F6.opPattern","COPY",BODY,{"derivedFrom":makeQuery(id+"F5.opPattern","COPY",BODY,{"derivedFrom":makeQuery(id+"F4.opPattern","COPY",BODY,{"derivedFrom":makeQuery(id+"F1.opRevolve","SWEPT_BODY",BODY,{"disambiguationData":[OSD([sQuery(id+"F0.wireOp",EDGE,"E1")])]}),"instanceName":"1"}),"instanceName":"1"}),"instanceName":"1"}),"instanceName":"1"});
            var Q214;
            Q214=makeQuery(id+"F10.opPattern","COPY",BODY,{"derivedFrom":makeQuery(id+"F6.opPattern","COPY",BODY,{"derivedFrom":makeQuery(id+"F5.opPattern","COPY",BODY,{"derivedFrom":makeQuery(id+"F4.opPattern","COPY",BODY,{"derivedFrom":makeQuery(id+"F2.opPattern","COPY",BODY,{"derivedFrom":makeQuery(id+"F1.opRevolve","SWEPT_BODY",BODY,{"disambiguationData":[OSD([sQuery(id+"F0.wireOp",EDGE,"E1")])]}),"instanceName":"1"}),"instanceName":"1"}),"instanceName":"1"}),"instanceName":"1"}),"instanceName":"1"});
            var Q215;
            Q215=makeQuery(id+"F10.opPattern","COPY",BODY,{"derivedFrom":makeQuery(id+"F6.opPattern","COPY",BODY,{"derivedFrom":makeQuery(id+"F5.opPattern","COPY",BODY,{"derivedFrom":makeQuery(id+"F4.opPattern","COPY",BODY,{"derivedFrom":makeQuery(id+"F3.opPattern","COPY",BODY,{"derivedFrom":makeQuery(id+"F2.opPattern","COPY",BODY,{"derivedFrom":makeQuery(id+"F1.opRevolve","SWEPT_BODY",BODY,{"disambiguationData":[OSD([sQuery(id+"F0.wireOp",EDGE,"E1")])]}),"instanceName":"1"}),"instanceName":"1"}),"instanceName":"1"}),"instanceName":"1"}),"instanceName":"1"}),"instanceName":"1"});
            var Q216;
            Q216=makeQuery(id+"F10.opPattern","COPY",BODY,{"derivedFrom":makeQuery(id+"F7.opPattern","COPY",BODY,{"derivedFrom":makeQuery(id+"F1.opRevolve","SWEPT_BODY",BODY,{"disambiguationData":[OSD([sQuery(id+"F0.wireOp",EDGE,"E1")])]}),"instanceName":"1"}),"instanceName":"1"});
            var Q217;
            Q217=makeQuery(id+"F10.opPattern","COPY",BODY,{"derivedFrom":makeQuery(id+"F7.opPattern","COPY",BODY,{"derivedFrom":makeQuery(id+"F2.opPattern","COPY",BODY,{"derivedFrom":makeQuery(id+"F1.opRevolve","SWEPT_BODY",BODY,{"disambiguationData":[OSD([sQuery(id+"F0.wireOp",EDGE,"E1")])]}),"instanceName":"1"}),"instanceName":"1"}),"instanceName":"1"});
            var Q218;
            Q218=makeQuery(id+"F10.opPattern","COPY",BODY,{"derivedFrom":makeQuery(id+"F7.opPattern","COPY",BODY,{"derivedFrom":makeQuery(id+"F3.opPattern","COPY",BODY,{"derivedFrom":makeQuery(id+"F2.opPattern","COPY",BODY,{"derivedFrom":makeQuery(id+"F1.opRevolve","SWEPT_BODY",BODY,{"disambiguationData":[OSD([sQuery(id+"F0.wireOp",EDGE,"E1")])]}),"instanceName":"1"}),"instanceName":"1"}),"instanceName":"1"}),"instanceName":"1"});
            var Q219;
            Q219=makeQuery(id+"F10.opPattern","COPY",BODY,{"derivedFrom":makeQuery(id+"F7.opPattern","COPY",BODY,{"derivedFrom":makeQuery(id+"F4.opPattern","COPY",BODY,{"derivedFrom":makeQuery(id+"F1.opRevolve","SWEPT_BODY",BODY,{"disambiguationData":[OSD([sQuery(id+"F0.wireOp",EDGE,"E1")])]}),"instanceName":"1"}),"instanceName":"1"}),"instanceName":"1"});
            var Q220;
            Q220=makeQuery(id+"F10.opPattern","COPY",BODY,{"derivedFrom":makeQuery(id+"F7.opPattern","COPY",BODY,{"derivedFrom":makeQuery(id+"F4.opPattern","COPY",BODY,{"derivedFrom":makeQuery(id+"F2.opPattern","COPY",BODY,{"derivedFrom":makeQuery(id+"F1.opRevolve","SWEPT_BODY",BODY,{"disambiguationData":[OSD([sQuery(id+"F0.wireOp",EDGE,"E1")])]}),"instanceName":"1"}),"instanceName":"1"}),"instanceName":"1"}),"instanceName":"1"});
            var Q221;
            Q221=makeQuery(id+"F10.opPattern","COPY",BODY,{"derivedFrom":makeQuery(id+"F7.opPattern","COPY",BODY,{"derivedFrom":makeQuery(id+"F4.opPattern","COPY",BODY,{"derivedFrom":makeQuery(id+"F3.opPattern","COPY",BODY,{"derivedFrom":makeQuery(id+"F2.opPattern","COPY",BODY,{"derivedFrom":makeQuery(id+"F1.opRevolve","SWEPT_BODY",BODY,{"disambiguationData":[OSD([sQuery(id+"F0.wireOp",EDGE,"E1")])]}),"instanceName":"1"}),"instanceName":"1"}),"instanceName":"1"}),"instanceName":"1"}),"instanceName":"1"});
            var Q222;
            Q222=makeQuery(id+"F10.opPattern","COPY",BODY,{"derivedFrom":makeQuery(id+"F7.opPattern","COPY",BODY,{"derivedFrom":makeQuery(id+"F5.opPattern","COPY",BODY,{"derivedFrom":makeQuery(id+"F1.opRevolve","SWEPT_BODY",BODY,{"disambiguationData":[OSD([sQuery(id+"F0.wireOp",EDGE,"E1")])]}),"instanceName":"1"}),"instanceName":"1"}),"instanceName":"1"});
            var Q223;
            Q223=makeQuery(id+"F10.opPattern","COPY",BODY,{"derivedFrom":makeQuery(id+"F7.opPattern","COPY",BODY,{"derivedFrom":makeQuery(id+"F5.opPattern","COPY",BODY,{"derivedFrom":makeQuery(id+"F2.opPattern","COPY",BODY,{"derivedFrom":makeQuery(id+"F1.opRevolve","SWEPT_BODY",BODY,{"disambiguationData":[OSD([sQuery(id+"F0.wireOp",EDGE,"E1")])]}),"instanceName":"1"}),"instanceName":"1"}),"instanceName":"1"}),"instanceName":"1"});
            var Q224;
            Q224=makeQuery(id+"F10.opPattern","COPY",BODY,{"derivedFrom":makeQuery(id+"F7.opPattern","COPY",BODY,{"derivedFrom":makeQuery(id+"F5.opPattern","COPY",BODY,{"derivedFrom":makeQuery(id+"F3.opPattern","COPY",BODY,{"derivedFrom":makeQuery(id+"F2.opPattern","COPY",BODY,{"derivedFrom":makeQuery(id+"F1.opRevolve","SWEPT_BODY",BODY,{"disambiguationData":[OSD([sQuery(id+"F0.wireOp",EDGE,"E1")])]}),"instanceName":"1"}),"instanceName":"1"}),"instanceName":"1"}),"instanceName":"1"}),"instanceName":"1"});
            var Q225;
            Q225=makeQuery(id+"F10.opPattern","COPY",BODY,{"derivedFrom":makeQuery(id+"F7.opPattern","COPY",BODY,{"derivedFrom":makeQuery(id+"F5.opPattern","COPY",BODY,{"derivedFrom":makeQuery(id+"F4.opPattern","COPY",BODY,{"derivedFrom":makeQuery(id+"F1.opRevolve","SWEPT_BODY",BODY,{"disambiguationData":[OSD([sQuery(id+"F0.wireOp",EDGE,"E1")])]}),"instanceName":"1"}),"instanceName":"1"}),"instanceName":"1"}),"instanceName":"1"});
            var Q226;
            Q226=makeQuery(id+"F10.opPattern","COPY",BODY,{"derivedFrom":makeQuery(id+"F7.opPattern","COPY",BODY,{"derivedFrom":makeQuery(id+"F5.opPattern","COPY",BODY,{"derivedFrom":makeQuery(id+"F4.opPattern","COPY",BODY,{"derivedFrom":makeQuery(id+"F2.opPattern","COPY",BODY,{"derivedFrom":makeQuery(id+"F1.opRevolve","SWEPT_BODY",BODY,{"disambiguationData":[OSD([sQuery(id+"F0.wireOp",EDGE,"E1")])]}),"instanceName":"1"}),"instanceName":"1"}),"instanceName":"1"}),"instanceName":"1"}),"instanceName":"1"});
            var Q227;
            Q227=makeQuery(id+"F10.opPattern","COPY",BODY,{"derivedFrom":makeQuery(id+"F7.opPattern","COPY",BODY,{"derivedFrom":makeQuery(id+"F5.opPattern","COPY",BODY,{"derivedFrom":makeQuery(id+"F4.opPattern","COPY",BODY,{"derivedFrom":makeQuery(id+"F3.opPattern","COPY",BODY,{"derivedFrom":makeQuery(id+"F2.opPattern","COPY",BODY,{"derivedFrom":makeQuery(id+"F1.opRevolve","SWEPT_BODY",BODY,{"disambiguationData":[OSD([sQuery(id+"F0.wireOp",EDGE,"E1")])]}),"instanceName":"1"}),"instanceName":"1"}),"instanceName":"1"}),"instanceName":"1"}),"instanceName":"1"}),"instanceName":"1"});
            var Q228;
            Q228=makeQuery(id+"F10.opPattern","COPY",BODY,{"derivedFrom":makeQuery(id+"F7.opPattern","COPY",BODY,{"derivedFrom":makeQuery(id+"F6.opPattern","COPY",BODY,{"derivedFrom":makeQuery(id+"F1.opRevolve","SWEPT_BODY",BODY,{"disambiguationData":[OSD([sQuery(id+"F0.wireOp",EDGE,"E1")])]}),"instanceName":"1"}),"instanceName":"1"}),"instanceName":"1"});
            var Q229;
            Q229=makeQuery(id+"F10.opPattern","COPY",BODY,{"derivedFrom":makeQuery(id+"F7.opPattern","COPY",BODY,{"derivedFrom":makeQuery(id+"F6.opPattern","COPY",BODY,{"derivedFrom":makeQuery(id+"F2.opPattern","COPY",BODY,{"derivedFrom":makeQuery(id+"F1.opRevolve","SWEPT_BODY",BODY,{"disambiguationData":[OSD([sQuery(id+"F0.wireOp",EDGE,"E1")])]}),"instanceName":"1"}),"instanceName":"1"}),"instanceName":"1"}),"instanceName":"1"});
            var Q230;
            Q230=makeQuery(id+"F10.opPattern","COPY",BODY,{"derivedFrom":makeQuery(id+"F7.opPattern","COPY",BODY,{"derivedFrom":makeQuery(id+"F6.opPattern","COPY",BODY,{"derivedFrom":makeQuery(id+"F3.opPattern","COPY",BODY,{"derivedFrom":makeQuery(id+"F2.opPattern","COPY",BODY,{"derivedFrom":makeQuery(id+"F1.opRevolve","SWEPT_BODY",BODY,{"disambiguationData":[OSD([sQuery(id+"F0.wireOp",EDGE,"E1")])]}),"instanceName":"1"}),"instanceName":"1"}),"instanceName":"1"}),"instanceName":"1"}),"instanceName":"1"});
            var Q231;
            Q231=makeQuery(id+"F10.opPattern","COPY",BODY,{"derivedFrom":makeQuery(id+"F7.opPattern","COPY",BODY,{"derivedFrom":makeQuery(id+"F6.opPattern","COPY",BODY,{"derivedFrom":makeQuery(id+"F4.opPattern","COPY",BODY,{"derivedFrom":makeQuery(id+"F1.opRevolve","SWEPT_BODY",BODY,{"disambiguationData":[OSD([sQuery(id+"F0.wireOp",EDGE,"E1")])]}),"instanceName":"1"}),"instanceName":"1"}),"instanceName":"1"}),"instanceName":"1"});
            var Q232;
            Q232=makeQuery(id+"F10.opPattern","COPY",BODY,{"derivedFrom":makeQuery(id+"F7.opPattern","COPY",BODY,{"derivedFrom":makeQuery(id+"F6.opPattern","COPY",BODY,{"derivedFrom":makeQuery(id+"F4.opPattern","COPY",BODY,{"derivedFrom":makeQuery(id+"F2.opPattern","COPY",BODY,{"derivedFrom":makeQuery(id+"F1.opRevolve","SWEPT_BODY",BODY,{"disambiguationData":[OSD([sQuery(id+"F0.wireOp",EDGE,"E1")])]}),"instanceName":"1"}),"instanceName":"1"}),"instanceName":"1"}),"instanceName":"1"}),"instanceName":"1"});
            var Q233;
            Q233=makeQuery(id+"F10.opPattern","COPY",BODY,{"derivedFrom":makeQuery(id+"F7.opPattern","COPY",BODY,{"derivedFrom":makeQuery(id+"F6.opPattern","COPY",BODY,{"derivedFrom":makeQuery(id+"F4.opPattern","COPY",BODY,{"derivedFrom":makeQuery(id+"F3.opPattern","COPY",BODY,{"derivedFrom":makeQuery(id+"F2.opPattern","COPY",BODY,{"derivedFrom":makeQuery(id+"F1.opRevolve","SWEPT_BODY",BODY,{"disambiguationData":[OSD([sQuery(id+"F0.wireOp",EDGE,"E1")])]}),"instanceName":"1"}),"instanceName":"1"}),"instanceName":"1"}),"instanceName":"1"}),"instanceName":"1"}),"instanceName":"1"});
            var Q234;
            Q234=makeQuery(id+"F10.opPattern","COPY",BODY,{"derivedFrom":makeQuery(id+"F7.opPattern","COPY",BODY,{"derivedFrom":makeQuery(id+"F6.opPattern","COPY",BODY,{"derivedFrom":makeQuery(id+"F5.opPattern","COPY",BODY,{"derivedFrom":makeQuery(id+"F1.opRevolve","SWEPT_BODY",BODY,{"disambiguationData":[OSD([sQuery(id+"F0.wireOp",EDGE,"E1")])]}),"instanceName":"1"}),"instanceName":"1"}),"instanceName":"1"}),"instanceName":"1"});
            var Q235;
            Q235=makeQuery(id+"F10.opPattern","COPY",BODY,{"derivedFrom":makeQuery(id+"F7.opPattern","COPY",BODY,{"derivedFrom":makeQuery(id+"F6.opPattern","COPY",BODY,{"derivedFrom":makeQuery(id+"F5.opPattern","COPY",BODY,{"derivedFrom":makeQuery(id+"F2.opPattern","COPY",BODY,{"derivedFrom":makeQuery(id+"F1.opRevolve","SWEPT_BODY",BODY,{"disambiguationData":[OSD([sQuery(id+"F0.wireOp",EDGE,"E1")])]}),"instanceName":"1"}),"instanceName":"1"}),"instanceName":"1"}),"instanceName":"1"}),"instanceName":"1"});
            var Q236;
            Q236=makeQuery(id+"F10.opPattern","COPY",BODY,{"derivedFrom":makeQuery(id+"F7.opPattern","COPY",BODY,{"derivedFrom":makeQuery(id+"F6.opPattern","COPY",BODY,{"derivedFrom":makeQuery(id+"F5.opPattern","COPY",BODY,{"derivedFrom":makeQuery(id+"F3.opPattern","COPY",BODY,{"derivedFrom":makeQuery(id+"F2.opPattern","COPY",BODY,{"derivedFrom":makeQuery(id+"F1.opRevolve","SWEPT_BODY",BODY,{"disambiguationData":[OSD([sQuery(id+"F0.wireOp",EDGE,"E1")])]}),"instanceName":"1"}),"instanceName":"1"}),"instanceName":"1"}),"instanceName":"1"}),"instanceName":"1"}),"instanceName":"1"});
            var Q237;
            Q237=makeQuery(id+"F10.opPattern","COPY",BODY,{"derivedFrom":makeQuery(id+"F7.opPattern","COPY",BODY,{"derivedFrom":makeQuery(id+"F6.opPattern","COPY",BODY,{"derivedFrom":makeQuery(id+"F5.opPattern","COPY",BODY,{"derivedFrom":makeQuery(id+"F4.opPattern","COPY",BODY,{"derivedFrom":makeQuery(id+"F1.opRevolve","SWEPT_BODY",BODY,{"disambiguationData":[OSD([sQuery(id+"F0.wireOp",EDGE,"E1")])]}),"instanceName":"1"}),"instanceName":"1"}),"instanceName":"1"}),"instanceName":"1"}),"instanceName":"1"});
            var Q238;
            Q238=makeQuery(id+"F10.opPattern","COPY",BODY,{"derivedFrom":makeQuery(id+"F7.opPattern","COPY",BODY,{"derivedFrom":makeQuery(id+"F6.opPattern","COPY",BODY,{"derivedFrom":makeQuery(id+"F5.opPattern","COPY",BODY,{"derivedFrom":makeQuery(id+"F4.opPattern","COPY",BODY,{"derivedFrom":makeQuery(id+"F2.opPattern","COPY",BODY,{"derivedFrom":makeQuery(id+"F1.opRevolve","SWEPT_BODY",BODY,{"disambiguationData":[OSD([sQuery(id+"F0.wireOp",EDGE,"E1")])]}),"instanceName":"1"}),"instanceName":"1"}),"instanceName":"1"}),"instanceName":"1"}),"instanceName":"1"}),"instanceName":"1"});
            var Q239;
            Q239=makeQuery(id+"F10.opPattern","COPY",BODY,{"derivedFrom":makeQuery(id+"F7.opPattern","COPY",BODY,{"derivedFrom":makeQuery(id+"F6.opPattern","COPY",BODY,{"derivedFrom":makeQuery(id+"F5.opPattern","COPY",BODY,{"derivedFrom":makeQuery(id+"F4.opPattern","COPY",BODY,{"derivedFrom":makeQuery(id+"F3.opPattern","COPY",BODY,{"derivedFrom":makeQuery(id+"F2.opPattern","COPY",BODY,{"derivedFrom":makeQuery(id+"F1.opRevolve","SWEPT_BODY",BODY,{"disambiguationData":[OSD([sQuery(id+"F0.wireOp",EDGE,"E1")])]}),"instanceName":"1"}),"instanceName":"1"}),"instanceName":"1"}),"instanceName":"1"}),"instanceName":"1"}),"instanceName":"1"}),"instanceName":"1"});
            var Q240;
            Q240=makeQuery(id+"F10.opPattern","COPY",BODY,{"derivedFrom":makeQuery(id+"F8.opPattern","COPY",BODY,{"derivedFrom":makeQuery(id+"F1.opRevolve","SWEPT_BODY",BODY,{"disambiguationData":[OSD([sQuery(id+"F0.wireOp",EDGE,"E1")])]}),"instanceName":"1"}),"instanceName":"1"});
            var Q241;
            Q241=makeQuery(id+"F10.opPattern","COPY",BODY,{"derivedFrom":makeQuery(id+"F8.opPattern","COPY",BODY,{"derivedFrom":makeQuery(id+"F2.opPattern","COPY",BODY,{"derivedFrom":makeQuery(id+"F1.opRevolve","SWEPT_BODY",BODY,{"disambiguationData":[OSD([sQuery(id+"F0.wireOp",EDGE,"E1")])]}),"instanceName":"1"}),"instanceName":"1"}),"instanceName":"1"});
            var Q242;
            Q242=makeQuery(id+"F10.opPattern","COPY",BODY,{"derivedFrom":makeQuery(id+"F8.opPattern","COPY",BODY,{"derivedFrom":makeQuery(id+"F3.opPattern","COPY",BODY,{"derivedFrom":makeQuery(id+"F2.opPattern","COPY",BODY,{"derivedFrom":makeQuery(id+"F1.opRevolve","SWEPT_BODY",BODY,{"disambiguationData":[OSD([sQuery(id+"F0.wireOp",EDGE,"E1")])]}),"instanceName":"1"}),"instanceName":"1"}),"instanceName":"1"}),"instanceName":"1"});
            var Q243;
            Q243=makeQuery(id+"F10.opPattern","COPY",BODY,{"derivedFrom":makeQuery(id+"F8.opPattern","COPY",BODY,{"derivedFrom":makeQuery(id+"F4.opPattern","COPY",BODY,{"derivedFrom":makeQuery(id+"F1.opRevolve","SWEPT_BODY",BODY,{"disambiguationData":[OSD([sQuery(id+"F0.wireOp",EDGE,"E1")])]}),"instanceName":"1"}),"instanceName":"1"}),"instanceName":"1"});
            var Q244;
            Q244=makeQuery(id+"F10.opPattern","COPY",BODY,{"derivedFrom":makeQuery(id+"F8.opPattern","COPY",BODY,{"derivedFrom":makeQuery(id+"F4.opPattern","COPY",BODY,{"derivedFrom":makeQuery(id+"F2.opPattern","COPY",BODY,{"derivedFrom":makeQuery(id+"F1.opRevolve","SWEPT_BODY",BODY,{"disambiguationData":[OSD([sQuery(id+"F0.wireOp",EDGE,"E1")])]}),"instanceName":"1"}),"instanceName":"1"}),"instanceName":"1"}),"instanceName":"1"});
            var Q245;
            Q245=makeQuery(id+"F10.opPattern","COPY",BODY,{"derivedFrom":makeQuery(id+"F8.opPattern","COPY",BODY,{"derivedFrom":makeQuery(id+"F4.opPattern","COPY",BODY,{"derivedFrom":makeQuery(id+"F3.opPattern","COPY",BODY,{"derivedFrom":makeQuery(id+"F2.opPattern","COPY",BODY,{"derivedFrom":makeQuery(id+"F1.opRevolve","SWEPT_BODY",BODY,{"disambiguationData":[OSD([sQuery(id+"F0.wireOp",EDGE,"E1")])]}),"instanceName":"1"}),"instanceName":"1"}),"instanceName":"1"}),"instanceName":"1"}),"instanceName":"1"});
            var Q246;
            Q246=makeQuery(id+"F10.opPattern","COPY",BODY,{"derivedFrom":makeQuery(id+"F8.opPattern","COPY",BODY,{"derivedFrom":makeQuery(id+"F5.opPattern","COPY",BODY,{"derivedFrom":makeQuery(id+"F1.opRevolve","SWEPT_BODY",BODY,{"disambiguationData":[OSD([sQuery(id+"F0.wireOp",EDGE,"E1")])]}),"instanceName":"1"}),"instanceName":"1"}),"instanceName":"1"});
            var Q247;
            Q247=makeQuery(id+"F10.opPattern","COPY",BODY,{"derivedFrom":makeQuery(id+"F8.opPattern","COPY",BODY,{"derivedFrom":makeQuery(id+"F5.opPattern","COPY",BODY,{"derivedFrom":makeQuery(id+"F2.opPattern","COPY",BODY,{"derivedFrom":makeQuery(id+"F1.opRevolve","SWEPT_BODY",BODY,{"disambiguationData":[OSD([sQuery(id+"F0.wireOp",EDGE,"E1")])]}),"instanceName":"1"}),"instanceName":"1"}),"instanceName":"1"}),"instanceName":"1"});
            var Q248;
            Q248=makeQuery(id+"F10.opPattern","COPY",BODY,{"derivedFrom":makeQuery(id+"F8.opPattern","COPY",BODY,{"derivedFrom":makeQuery(id+"F5.opPattern","COPY",BODY,{"derivedFrom":makeQuery(id+"F3.opPattern","COPY",BODY,{"derivedFrom":makeQuery(id+"F2.opPattern","COPY",BODY,{"derivedFrom":makeQuery(id+"F1.opRevolve","SWEPT_BODY",BODY,{"disambiguationData":[OSD([sQuery(id+"F0.wireOp",EDGE,"E1")])]}),"instanceName":"1"}),"instanceName":"1"}),"instanceName":"1"}),"instanceName":"1"}),"instanceName":"1"});
            var Q249;
            Q249=makeQuery(id+"F10.opPattern","COPY",BODY,{"derivedFrom":makeQuery(id+"F8.opPattern","COPY",BODY,{"derivedFrom":makeQuery(id+"F5.opPattern","COPY",BODY,{"derivedFrom":makeQuery(id+"F4.opPattern","COPY",BODY,{"derivedFrom":makeQuery(id+"F1.opRevolve","SWEPT_BODY",BODY,{"disambiguationData":[OSD([sQuery(id+"F0.wireOp",EDGE,"E1")])]}),"instanceName":"1"}),"instanceName":"1"}),"instanceName":"1"}),"instanceName":"1"});
            var Q250;
            Q250=makeQuery(id+"F10.opPattern","COPY",BODY,{"derivedFrom":makeQuery(id+"F8.opPattern","COPY",BODY,{"derivedFrom":makeQuery(id+"F5.opPattern","COPY",BODY,{"derivedFrom":makeQuery(id+"F4.opPattern","COPY",BODY,{"derivedFrom":makeQuery(id+"F2.opPattern","COPY",BODY,{"derivedFrom":makeQuery(id+"F1.opRevolve","SWEPT_BODY",BODY,{"disambiguationData":[OSD([sQuery(id+"F0.wireOp",EDGE,"E1")])]}),"instanceName":"1"}),"instanceName":"1"}),"instanceName":"1"}),"instanceName":"1"}),"instanceName":"1"});
            var Q251;
            Q251=makeQuery(id+"F10.opPattern","COPY",BODY,{"derivedFrom":makeQuery(id+"F8.opPattern","COPY",BODY,{"derivedFrom":makeQuery(id+"F5.opPattern","COPY",BODY,{"derivedFrom":makeQuery(id+"F4.opPattern","COPY",BODY,{"derivedFrom":makeQuery(id+"F3.opPattern","COPY",BODY,{"derivedFrom":makeQuery(id+"F2.opPattern","COPY",BODY,{"derivedFrom":makeQuery(id+"F1.opRevolve","SWEPT_BODY",BODY,{"disambiguationData":[OSD([sQuery(id+"F0.wireOp",EDGE,"E1")])]}),"instanceName":"1"}),"instanceName":"1"}),"instanceName":"1"}),"instanceName":"1"}),"instanceName":"1"}),"instanceName":"1"});
            var Q252;
            Q252=makeQuery(id+"F10.opPattern","COPY",BODY,{"derivedFrom":makeQuery(id+"F8.opPattern","COPY",BODY,{"derivedFrom":makeQuery(id+"F6.opPattern","COPY",BODY,{"derivedFrom":makeQuery(id+"F1.opRevolve","SWEPT_BODY",BODY,{"disambiguationData":[OSD([sQuery(id+"F0.wireOp",EDGE,"E1")])]}),"instanceName":"1"}),"instanceName":"1"}),"instanceName":"1"});
            var Q253;
            Q253=makeQuery(id+"F10.opPattern","COPY",BODY,{"derivedFrom":makeQuery(id+"F8.opPattern","COPY",BODY,{"derivedFrom":makeQuery(id+"F6.opPattern","COPY",BODY,{"derivedFrom":makeQuery(id+"F2.opPattern","COPY",BODY,{"derivedFrom":makeQuery(id+"F1.opRevolve","SWEPT_BODY",BODY,{"disambiguationData":[OSD([sQuery(id+"F0.wireOp",EDGE,"E1")])]}),"instanceName":"1"}),"instanceName":"1"}),"instanceName":"1"}),"instanceName":"1"});
            var Q254;
            Q254=makeQuery(id+"F10.opPattern","COPY",BODY,{"derivedFrom":makeQuery(id+"F8.opPattern","COPY",BODY,{"derivedFrom":makeQuery(id+"F6.opPattern","COPY",BODY,{"derivedFrom":makeQuery(id+"F3.opPattern","COPY",BODY,{"derivedFrom":makeQuery(id+"F2.opPattern","COPY",BODY,{"derivedFrom":makeQuery(id+"F1.opRevolve","SWEPT_BODY",BODY,{"disambiguationData":[OSD([sQuery(id+"F0.wireOp",EDGE,"E1")])]}),"instanceName":"1"}),"instanceName":"1"}),"instanceName":"1"}),"instanceName":"1"}),"instanceName":"1"});
            var Q255;
            Q255=makeQuery(id+"F10.opPattern","COPY",BODY,{"derivedFrom":makeQuery(id+"F8.opPattern","COPY",BODY,{"derivedFrom":makeQuery(id+"F6.opPattern","COPY",BODY,{"derivedFrom":makeQuery(id+"F4.opPattern","COPY",BODY,{"derivedFrom":makeQuery(id+"F1.opRevolve","SWEPT_BODY",BODY,{"disambiguationData":[OSD([sQuery(id+"F0.wireOp",EDGE,"E1")])]}),"instanceName":"1"}),"instanceName":"1"}),"instanceName":"1"}),"instanceName":"1"});
            var Q256;
            Q256=makeQuery(id+"F10.opPattern","COPY",BODY,{"derivedFrom":makeQuery(id+"F8.opPattern","COPY",BODY,{"derivedFrom":makeQuery(id+"F6.opPattern","COPY",BODY,{"derivedFrom":makeQuery(id+"F4.opPattern","COPY",BODY,{"derivedFrom":makeQuery(id+"F2.opPattern","COPY",BODY,{"derivedFrom":makeQuery(id+"F1.opRevolve","SWEPT_BODY",BODY,{"disambiguationData":[OSD([sQuery(id+"F0.wireOp",EDGE,"E1")])]}),"instanceName":"1"}),"instanceName":"1"}),"instanceName":"1"}),"instanceName":"1"}),"instanceName":"1"});
            var Q257;
            Q257=makeQuery(id+"F10.opPattern","COPY",BODY,{"derivedFrom":makeQuery(id+"F8.opPattern","COPY",BODY,{"derivedFrom":makeQuery(id+"F6.opPattern","COPY",BODY,{"derivedFrom":makeQuery(id+"F4.opPattern","COPY",BODY,{"derivedFrom":makeQuery(id+"F3.opPattern","COPY",BODY,{"derivedFrom":makeQuery(id+"F2.opPattern","COPY",BODY,{"derivedFrom":makeQuery(id+"F1.opRevolve","SWEPT_BODY",BODY,{"disambiguationData":[OSD([sQuery(id+"F0.wireOp",EDGE,"E1")])]}),"instanceName":"1"}),"instanceName":"1"}),"instanceName":"1"}),"instanceName":"1"}),"instanceName":"1"}),"instanceName":"1"});
            var Q258;
            Q258=makeQuery(id+"F10.opPattern","COPY",BODY,{"derivedFrom":makeQuery(id+"F8.opPattern","COPY",BODY,{"derivedFrom":makeQuery(id+"F6.opPattern","COPY",BODY,{"derivedFrom":makeQuery(id+"F5.opPattern","COPY",BODY,{"derivedFrom":makeQuery(id+"F1.opRevolve","SWEPT_BODY",BODY,{"disambiguationData":[OSD([sQuery(id+"F0.wireOp",EDGE,"E1")])]}),"instanceName":"1"}),"instanceName":"1"}),"instanceName":"1"}),"instanceName":"1"});
            var Q259;
            Q259=makeQuery(id+"F10.opPattern","COPY",BODY,{"derivedFrom":makeQuery(id+"F8.opPattern","COPY",BODY,{"derivedFrom":makeQuery(id+"F6.opPattern","COPY",BODY,{"derivedFrom":makeQuery(id+"F5.opPattern","COPY",BODY,{"derivedFrom":makeQuery(id+"F2.opPattern","COPY",BODY,{"derivedFrom":makeQuery(id+"F1.opRevolve","SWEPT_BODY",BODY,{"disambiguationData":[OSD([sQuery(id+"F0.wireOp",EDGE,"E1")])]}),"instanceName":"1"}),"instanceName":"1"}),"instanceName":"1"}),"instanceName":"1"}),"instanceName":"1"});
            var Q260;
            Q260=makeQuery(id+"F10.opPattern","COPY",BODY,{"derivedFrom":makeQuery(id+"F8.opPattern","COPY",BODY,{"derivedFrom":makeQuery(id+"F6.opPattern","COPY",BODY,{"derivedFrom":makeQuery(id+"F5.opPattern","COPY",BODY,{"derivedFrom":makeQuery(id+"F3.opPattern","COPY",BODY,{"derivedFrom":makeQuery(id+"F2.opPattern","COPY",BODY,{"derivedFrom":makeQuery(id+"F1.opRevolve","SWEPT_BODY",BODY,{"disambiguationData":[OSD([sQuery(id+"F0.wireOp",EDGE,"E1")])]}),"instanceName":"1"}),"instanceName":"1"}),"instanceName":"1"}),"instanceName":"1"}),"instanceName":"1"}),"instanceName":"1"});
            var Q261;
            Q261=makeQuery(id+"F10.opPattern","COPY",BODY,{"derivedFrom":makeQuery(id+"F8.opPattern","COPY",BODY,{"derivedFrom":makeQuery(id+"F6.opPattern","COPY",BODY,{"derivedFrom":makeQuery(id+"F5.opPattern","COPY",BODY,{"derivedFrom":makeQuery(id+"F4.opPattern","COPY",BODY,{"derivedFrom":makeQuery(id+"F1.opRevolve","SWEPT_BODY",BODY,{"disambiguationData":[OSD([sQuery(id+"F0.wireOp",EDGE,"E1")])]}),"instanceName":"1"}),"instanceName":"1"}),"instanceName":"1"}),"instanceName":"1"}),"instanceName":"1"});
            var Q262;
            Q262=makeQuery(id+"F10.opPattern","COPY",BODY,{"derivedFrom":makeQuery(id+"F8.opPattern","COPY",BODY,{"derivedFrom":makeQuery(id+"F6.opPattern","COPY",BODY,{"derivedFrom":makeQuery(id+"F5.opPattern","COPY",BODY,{"derivedFrom":makeQuery(id+"F4.opPattern","COPY",BODY,{"derivedFrom":makeQuery(id+"F2.opPattern","COPY",BODY,{"derivedFrom":makeQuery(id+"F1.opRevolve","SWEPT_BODY",BODY,{"disambiguationData":[OSD([sQuery(id+"F0.wireOp",EDGE,"E1")])]}),"instanceName":"1"}),"instanceName":"1"}),"instanceName":"1"}),"instanceName":"1"}),"instanceName":"1"}),"instanceName":"1"});
            var Q263;
            Q263=makeQuery(id+"F10.opPattern","COPY",BODY,{"derivedFrom":makeQuery(id+"F8.opPattern","COPY",BODY,{"derivedFrom":makeQuery(id+"F6.opPattern","COPY",BODY,{"derivedFrom":makeQuery(id+"F5.opPattern","COPY",BODY,{"derivedFrom":makeQuery(id+"F4.opPattern","COPY",BODY,{"derivedFrom":makeQuery(id+"F3.opPattern","COPY",BODY,{"derivedFrom":makeQuery(id+"F2.opPattern","COPY",BODY,{"derivedFrom":makeQuery(id+"F1.opRevolve","SWEPT_BODY",BODY,{"disambiguationData":[OSD([sQuery(id+"F0.wireOp",EDGE,"E1")])]}),"instanceName":"1"}),"instanceName":"1"}),"instanceName":"1"}),"instanceName":"1"}),"instanceName":"1"}),"instanceName":"1"}),"instanceName":"1"});
            var Q264;
            Q264=makeQuery(id+"F10.opPattern","COPY",BODY,{"derivedFrom":makeQuery(id+"F8.opPattern","COPY",BODY,{"derivedFrom":makeQuery(id+"F7.opPattern","COPY",BODY,{"derivedFrom":makeQuery(id+"F1.opRevolve","SWEPT_BODY",BODY,{"disambiguationData":[OSD([sQuery(id+"F0.wireOp",EDGE,"E1")])]}),"instanceName":"1"}),"instanceName":"1"}),"instanceName":"1"});
            var Q265;
            Q265=makeQuery(id+"F10.opPattern","COPY",BODY,{"derivedFrom":makeQuery(id+"F8.opPattern","COPY",BODY,{"derivedFrom":makeQuery(id+"F7.opPattern","COPY",BODY,{"derivedFrom":makeQuery(id+"F2.opPattern","COPY",BODY,{"derivedFrom":makeQuery(id+"F1.opRevolve","SWEPT_BODY",BODY,{"disambiguationData":[OSD([sQuery(id+"F0.wireOp",EDGE,"E1")])]}),"instanceName":"1"}),"instanceName":"1"}),"instanceName":"1"}),"instanceName":"1"});
            var Q266;
            Q266=makeQuery(id+"F10.opPattern","COPY",BODY,{"derivedFrom":makeQuery(id+"F8.opPattern","COPY",BODY,{"derivedFrom":makeQuery(id+"F7.opPattern","COPY",BODY,{"derivedFrom":makeQuery(id+"F3.opPattern","COPY",BODY,{"derivedFrom":makeQuery(id+"F2.opPattern","COPY",BODY,{"derivedFrom":makeQuery(id+"F1.opRevolve","SWEPT_BODY",BODY,{"disambiguationData":[OSD([sQuery(id+"F0.wireOp",EDGE,"E1")])]}),"instanceName":"1"}),"instanceName":"1"}),"instanceName":"1"}),"instanceName":"1"}),"instanceName":"1"});
            var Q267;
            Q267=makeQuery(id+"F10.opPattern","COPY",BODY,{"derivedFrom":makeQuery(id+"F8.opPattern","COPY",BODY,{"derivedFrom":makeQuery(id+"F7.opPattern","COPY",BODY,{"derivedFrom":makeQuery(id+"F4.opPattern","COPY",BODY,{"derivedFrom":makeQuery(id+"F1.opRevolve","SWEPT_BODY",BODY,{"disambiguationData":[OSD([sQuery(id+"F0.wireOp",EDGE,"E1")])]}),"instanceName":"1"}),"instanceName":"1"}),"instanceName":"1"}),"instanceName":"1"});
            var Q268;
            Q268=makeQuery(id+"F10.opPattern","COPY",BODY,{"derivedFrom":makeQuery(id+"F8.opPattern","COPY",BODY,{"derivedFrom":makeQuery(id+"F7.opPattern","COPY",BODY,{"derivedFrom":makeQuery(id+"F4.opPattern","COPY",BODY,{"derivedFrom":makeQuery(id+"F2.opPattern","COPY",BODY,{"derivedFrom":makeQuery(id+"F1.opRevolve","SWEPT_BODY",BODY,{"disambiguationData":[OSD([sQuery(id+"F0.wireOp",EDGE,"E1")])]}),"instanceName":"1"}),"instanceName":"1"}),"instanceName":"1"}),"instanceName":"1"}),"instanceName":"1"});
            var Q269;
            Q269=makeQuery(id+"F10.opPattern","COPY",BODY,{"derivedFrom":makeQuery(id+"F8.opPattern","COPY",BODY,{"derivedFrom":makeQuery(id+"F7.opPattern","COPY",BODY,{"derivedFrom":makeQuery(id+"F4.opPattern","COPY",BODY,{"derivedFrom":makeQuery(id+"F3.opPattern","COPY",BODY,{"derivedFrom":makeQuery(id+"F2.opPattern","COPY",BODY,{"derivedFrom":makeQuery(id+"F1.opRevolve","SWEPT_BODY",BODY,{"disambiguationData":[OSD([sQuery(id+"F0.wireOp",EDGE,"E1")])]}),"instanceName":"1"}),"instanceName":"1"}),"instanceName":"1"}),"instanceName":"1"}),"instanceName":"1"}),"instanceName":"1"});
            var Q270;
            Q270=makeQuery(id+"F10.opPattern","COPY",BODY,{"derivedFrom":makeQuery(id+"F8.opPattern","COPY",BODY,{"derivedFrom":makeQuery(id+"F7.opPattern","COPY",BODY,{"derivedFrom":makeQuery(id+"F5.opPattern","COPY",BODY,{"derivedFrom":makeQuery(id+"F1.opRevolve","SWEPT_BODY",BODY,{"disambiguationData":[OSD([sQuery(id+"F0.wireOp",EDGE,"E1")])]}),"instanceName":"1"}),"instanceName":"1"}),"instanceName":"1"}),"instanceName":"1"});
            var Q271;
            Q271=makeQuery(id+"F10.opPattern","COPY",BODY,{"derivedFrom":makeQuery(id+"F8.opPattern","COPY",BODY,{"derivedFrom":makeQuery(id+"F7.opPattern","COPY",BODY,{"derivedFrom":makeQuery(id+"F5.opPattern","COPY",BODY,{"derivedFrom":makeQuery(id+"F2.opPattern","COPY",BODY,{"derivedFrom":makeQuery(id+"F1.opRevolve","SWEPT_BODY",BODY,{"disambiguationData":[OSD([sQuery(id+"F0.wireOp",EDGE,"E1")])]}),"instanceName":"1"}),"instanceName":"1"}),"instanceName":"1"}),"instanceName":"1"}),"instanceName":"1"});
            var Q272;
            Q272=makeQuery(id+"F10.opPattern","COPY",BODY,{"derivedFrom":makeQuery(id+"F8.opPattern","COPY",BODY,{"derivedFrom":makeQuery(id+"F7.opPattern","COPY",BODY,{"derivedFrom":makeQuery(id+"F5.opPattern","COPY",BODY,{"derivedFrom":makeQuery(id+"F3.opPattern","COPY",BODY,{"derivedFrom":makeQuery(id+"F2.opPattern","COPY",BODY,{"derivedFrom":makeQuery(id+"F1.opRevolve","SWEPT_BODY",BODY,{"disambiguationData":[OSD([sQuery(id+"F0.wireOp",EDGE,"E1")])]}),"instanceName":"1"}),"instanceName":"1"}),"instanceName":"1"}),"instanceName":"1"}),"instanceName":"1"}),"instanceName":"1"});
            var Q273;
            Q273=makeQuery(id+"F10.opPattern","COPY",BODY,{"derivedFrom":makeQuery(id+"F8.opPattern","COPY",BODY,{"derivedFrom":makeQuery(id+"F7.opPattern","COPY",BODY,{"derivedFrom":makeQuery(id+"F5.opPattern","COPY",BODY,{"derivedFrom":makeQuery(id+"F4.opPattern","COPY",BODY,{"derivedFrom":makeQuery(id+"F1.opRevolve","SWEPT_BODY",BODY,{"disambiguationData":[OSD([sQuery(id+"F0.wireOp",EDGE,"E1")])]}),"instanceName":"1"}),"instanceName":"1"}),"instanceName":"1"}),"instanceName":"1"}),"instanceName":"1"});
            var Q274;
            Q274=makeQuery(id+"F10.opPattern","COPY",BODY,{"derivedFrom":makeQuery(id+"F8.opPattern","COPY",BODY,{"derivedFrom":makeQuery(id+"F7.opPattern","COPY",BODY,{"derivedFrom":makeQuery(id+"F5.opPattern","COPY",BODY,{"derivedFrom":makeQuery(id+"F4.opPattern","COPY",BODY,{"derivedFrom":makeQuery(id+"F2.opPattern","COPY",BODY,{"derivedFrom":makeQuery(id+"F1.opRevolve","SWEPT_BODY",BODY,{"disambiguationData":[OSD([sQuery(id+"F0.wireOp",EDGE,"E1")])]}),"instanceName":"1"}),"instanceName":"1"}),"instanceName":"1"}),"instanceName":"1"}),"instanceName":"1"}),"instanceName":"1"});
            var Q275;
            Q275=makeQuery(id+"F10.opPattern","COPY",BODY,{"derivedFrom":makeQuery(id+"F8.opPattern","COPY",BODY,{"derivedFrom":makeQuery(id+"F7.opPattern","COPY",BODY,{"derivedFrom":makeQuery(id+"F5.opPattern","COPY",BODY,{"derivedFrom":makeQuery(id+"F4.opPattern","COPY",BODY,{"derivedFrom":makeQuery(id+"F3.opPattern","COPY",BODY,{"derivedFrom":makeQuery(id+"F2.opPattern","COPY",BODY,{"derivedFrom":makeQuery(id+"F1.opRevolve","SWEPT_BODY",BODY,{"disambiguationData":[OSD([sQuery(id+"F0.wireOp",EDGE,"E1")])]}),"instanceName":"1"}),"instanceName":"1"}),"instanceName":"1"}),"instanceName":"1"}),"instanceName":"1"}),"instanceName":"1"}),"instanceName":"1"});
            var Q276;
            Q276=makeQuery(id+"F10.opPattern","COPY",BODY,{"derivedFrom":makeQuery(id+"F8.opPattern","COPY",BODY,{"derivedFrom":makeQuery(id+"F7.opPattern","COPY",BODY,{"derivedFrom":makeQuery(id+"F6.opPattern","COPY",BODY,{"derivedFrom":makeQuery(id+"F1.opRevolve","SWEPT_BODY",BODY,{"disambiguationData":[OSD([sQuery(id+"F0.wireOp",EDGE,"E1")])]}),"instanceName":"1"}),"instanceName":"1"}),"instanceName":"1"}),"instanceName":"1"});
            var Q277;
            Q277=makeQuery(id+"F10.opPattern","COPY",BODY,{"derivedFrom":makeQuery(id+"F8.opPattern","COPY",BODY,{"derivedFrom":makeQuery(id+"F7.opPattern","COPY",BODY,{"derivedFrom":makeQuery(id+"F6.opPattern","COPY",BODY,{"derivedFrom":makeQuery(id+"F2.opPattern","COPY",BODY,{"derivedFrom":makeQuery(id+"F1.opRevolve","SWEPT_BODY",BODY,{"disambiguationData":[OSD([sQuery(id+"F0.wireOp",EDGE,"E1")])]}),"instanceName":"1"}),"instanceName":"1"}),"instanceName":"1"}),"instanceName":"1"}),"instanceName":"1"});
            var Q278;
            Q278=makeQuery(id+"F10.opPattern","COPY",BODY,{"derivedFrom":makeQuery(id+"F8.opPattern","COPY",BODY,{"derivedFrom":makeQuery(id+"F7.opPattern","COPY",BODY,{"derivedFrom":makeQuery(id+"F6.opPattern","COPY",BODY,{"derivedFrom":makeQuery(id+"F3.opPattern","COPY",BODY,{"derivedFrom":makeQuery(id+"F2.opPattern","COPY",BODY,{"derivedFrom":makeQuery(id+"F1.opRevolve","SWEPT_BODY",BODY,{"disambiguationData":[OSD([sQuery(id+"F0.wireOp",EDGE,"E1")])]}),"instanceName":"1"}),"instanceName":"1"}),"instanceName":"1"}),"instanceName":"1"}),"instanceName":"1"}),"instanceName":"1"});
            var Q279;
            Q279=makeQuery(id+"F10.opPattern","COPY",BODY,{"derivedFrom":makeQuery(id+"F8.opPattern","COPY",BODY,{"derivedFrom":makeQuery(id+"F7.opPattern","COPY",BODY,{"derivedFrom":makeQuery(id+"F6.opPattern","COPY",BODY,{"derivedFrom":makeQuery(id+"F4.opPattern","COPY",BODY,{"derivedFrom":makeQuery(id+"F1.opRevolve","SWEPT_BODY",BODY,{"disambiguationData":[OSD([sQuery(id+"F0.wireOp",EDGE,"E1")])]}),"instanceName":"1"}),"instanceName":"1"}),"instanceName":"1"}),"instanceName":"1"}),"instanceName":"1"});
            var Q280;
            Q280=makeQuery(id+"F10.opPattern","COPY",BODY,{"derivedFrom":makeQuery(id+"F8.opPattern","COPY",BODY,{"derivedFrom":makeQuery(id+"F7.opPattern","COPY",BODY,{"derivedFrom":makeQuery(id+"F6.opPattern","COPY",BODY,{"derivedFrom":makeQuery(id+"F4.opPattern","COPY",BODY,{"derivedFrom":makeQuery(id+"F2.opPattern","COPY",BODY,{"derivedFrom":makeQuery(id+"F1.opRevolve","SWEPT_BODY",BODY,{"disambiguationData":[OSD([sQuery(id+"F0.wireOp",EDGE,"E1")])]}),"instanceName":"1"}),"instanceName":"1"}),"instanceName":"1"}),"instanceName":"1"}),"instanceName":"1"}),"instanceName":"1"});
            var Q281;
            Q281=makeQuery(id+"F10.opPattern","COPY",BODY,{"derivedFrom":makeQuery(id+"F8.opPattern","COPY",BODY,{"derivedFrom":makeQuery(id+"F7.opPattern","COPY",BODY,{"derivedFrom":makeQuery(id+"F6.opPattern","COPY",BODY,{"derivedFrom":makeQuery(id+"F4.opPattern","COPY",BODY,{"derivedFrom":makeQuery(id+"F3.opPattern","COPY",BODY,{"derivedFrom":makeQuery(id+"F2.opPattern","COPY",BODY,{"derivedFrom":makeQuery(id+"F1.opRevolve","SWEPT_BODY",BODY,{"disambiguationData":[OSD([sQuery(id+"F0.wireOp",EDGE,"E1")])]}),"instanceName":"1"}),"instanceName":"1"}),"instanceName":"1"}),"instanceName":"1"}),"instanceName":"1"}),"instanceName":"1"}),"instanceName":"1"});
            var Q282;
            Q282=makeQuery(id+"F10.opPattern","COPY",BODY,{"derivedFrom":makeQuery(id+"F8.opPattern","COPY",BODY,{"derivedFrom":makeQuery(id+"F7.opPattern","COPY",BODY,{"derivedFrom":makeQuery(id+"F6.opPattern","COPY",BODY,{"derivedFrom":makeQuery(id+"F5.opPattern","COPY",BODY,{"derivedFrom":makeQuery(id+"F1.opRevolve","SWEPT_BODY",BODY,{"disambiguationData":[OSD([sQuery(id+"F0.wireOp",EDGE,"E1")])]}),"instanceName":"1"}),"instanceName":"1"}),"instanceName":"1"}),"instanceName":"1"}),"instanceName":"1"});
            var Q283;
            Q283=makeQuery(id+"F10.opPattern","COPY",BODY,{"derivedFrom":makeQuery(id+"F8.opPattern","COPY",BODY,{"derivedFrom":makeQuery(id+"F7.opPattern","COPY",BODY,{"derivedFrom":makeQuery(id+"F6.opPattern","COPY",BODY,{"derivedFrom":makeQuery(id+"F5.opPattern","COPY",BODY,{"derivedFrom":makeQuery(id+"F2.opPattern","COPY",BODY,{"derivedFrom":makeQuery(id+"F1.opRevolve","SWEPT_BODY",BODY,{"disambiguationData":[OSD([sQuery(id+"F0.wireOp",EDGE,"E1")])]}),"instanceName":"1"}),"instanceName":"1"}),"instanceName":"1"}),"instanceName":"1"}),"instanceName":"1"}),"instanceName":"1"});
            var Q284;
            Q284=makeQuery(id+"F10.opPattern","COPY",BODY,{"derivedFrom":makeQuery(id+"F8.opPattern","COPY",BODY,{"derivedFrom":makeQuery(id+"F7.opPattern","COPY",BODY,{"derivedFrom":makeQuery(id+"F6.opPattern","COPY",BODY,{"derivedFrom":makeQuery(id+"F5.opPattern","COPY",BODY,{"derivedFrom":makeQuery(id+"F3.opPattern","COPY",BODY,{"derivedFrom":makeQuery(id+"F2.opPattern","COPY",BODY,{"derivedFrom":makeQuery(id+"F1.opRevolve","SWEPT_BODY",BODY,{"disambiguationData":[OSD([sQuery(id+"F0.wireOp",EDGE,"E1")])]}),"instanceName":"1"}),"instanceName":"1"}),"instanceName":"1"}),"instanceName":"1"}),"instanceName":"1"}),"instanceName":"1"}),"instanceName":"1"});
            var Q285;
            Q285=makeQuery(id+"F10.opPattern","COPY",BODY,{"derivedFrom":makeQuery(id+"F8.opPattern","COPY",BODY,{"derivedFrom":makeQuery(id+"F7.opPattern","COPY",BODY,{"derivedFrom":makeQuery(id+"F6.opPattern","COPY",BODY,{"derivedFrom":makeQuery(id+"F5.opPattern","COPY",BODY,{"derivedFrom":makeQuery(id+"F4.opPattern","COPY",BODY,{"derivedFrom":makeQuery(id+"F1.opRevolve","SWEPT_BODY",BODY,{"disambiguationData":[OSD([sQuery(id+"F0.wireOp",EDGE,"E1")])]}),"instanceName":"1"}),"instanceName":"1"}),"instanceName":"1"}),"instanceName":"1"}),"instanceName":"1"}),"instanceName":"1"});
            var Q286;
            Q286=makeQuery(id+"F10.opPattern","COPY",BODY,{"derivedFrom":makeQuery(id+"F8.opPattern","COPY",BODY,{"derivedFrom":makeQuery(id+"F7.opPattern","COPY",BODY,{"derivedFrom":makeQuery(id+"F6.opPattern","COPY",BODY,{"derivedFrom":makeQuery(id+"F5.opPattern","COPY",BODY,{"derivedFrom":makeQuery(id+"F4.opPattern","COPY",BODY,{"derivedFrom":makeQuery(id+"F2.opPattern","COPY",BODY,{"derivedFrom":makeQuery(id+"F1.opRevolve","SWEPT_BODY",BODY,{"disambiguationData":[OSD([sQuery(id+"F0.wireOp",EDGE,"E1")])]}),"instanceName":"1"}),"instanceName":"1"}),"instanceName":"1"}),"instanceName":"1"}),"instanceName":"1"}),"instanceName":"1"}),"instanceName":"1"});
            var Q287;
            Q287=makeQuery(id+"F10.opPattern","COPY",BODY,{"derivedFrom":makeQuery(id+"F8.opPattern","COPY",BODY,{"derivedFrom":makeQuery(id+"F7.opPattern","COPY",BODY,{"derivedFrom":makeQuery(id+"F6.opPattern","COPY",BODY,{"derivedFrom":makeQuery(id+"F5.opPattern","COPY",BODY,{"derivedFrom":makeQuery(id+"F4.opPattern","COPY",BODY,{"derivedFrom":makeQuery(id+"F3.opPattern","COPY",BODY,{"derivedFrom":makeQuery(id+"F2.opPattern","COPY",BODY,{"derivedFrom":makeQuery(id+"F1.opRevolve","SWEPT_BODY",BODY,{"disambiguationData":[OSD([sQuery(id+"F0.wireOp",EDGE,"E1")])]}),"instanceName":"1"}),"instanceName":"1"}),"instanceName":"1"}),"instanceName":"1"}),"instanceName":"1"}),"instanceName":"1"}),"instanceName":"1"}),"instanceName":"1"});
            var Q288;
            Q288=makeQuery(id+"F10.opPattern","COPY",BODY,{"derivedFrom":makeQuery(id+"F9.opPattern","COPY",BODY,{"derivedFrom":makeQuery(id+"F1.opRevolve","SWEPT_BODY",BODY,{"disambiguationData":[OSD([sQuery(id+"F0.wireOp",EDGE,"E1")])]}),"instanceName":"1"}),"instanceName":"1"});
            var Q289;
            Q289=makeQuery(id+"F10.opPattern","COPY",BODY,{"derivedFrom":makeQuery(id+"F9.opPattern","COPY",BODY,{"derivedFrom":makeQuery(id+"F2.opPattern","COPY",BODY,{"derivedFrom":makeQuery(id+"F1.opRevolve","SWEPT_BODY",BODY,{"disambiguationData":[OSD([sQuery(id+"F0.wireOp",EDGE,"E1")])]}),"instanceName":"1"}),"instanceName":"1"}),"instanceName":"1"});
            var Q290;
            Q290=makeQuery(id+"F10.opPattern","COPY",BODY,{"derivedFrom":makeQuery(id+"F9.opPattern","COPY",BODY,{"derivedFrom":makeQuery(id+"F3.opPattern","COPY",BODY,{"derivedFrom":makeQuery(id+"F2.opPattern","COPY",BODY,{"derivedFrom":makeQuery(id+"F1.opRevolve","SWEPT_BODY",BODY,{"disambiguationData":[OSD([sQuery(id+"F0.wireOp",EDGE,"E1")])]}),"instanceName":"1"}),"instanceName":"1"}),"instanceName":"1"}),"instanceName":"1"});
            var Q291;
            Q291=makeQuery(id+"F10.opPattern","COPY",BODY,{"derivedFrom":makeQuery(id+"F9.opPattern","COPY",BODY,{"derivedFrom":makeQuery(id+"F4.opPattern","COPY",BODY,{"derivedFrom":makeQuery(id+"F1.opRevolve","SWEPT_BODY",BODY,{"disambiguationData":[OSD([sQuery(id+"F0.wireOp",EDGE,"E1")])]}),"instanceName":"1"}),"instanceName":"1"}),"instanceName":"1"});
            var Q292;
            Q292=makeQuery(id+"F10.opPattern","COPY",BODY,{"derivedFrom":makeQuery(id+"F9.opPattern","COPY",BODY,{"derivedFrom":makeQuery(id+"F4.opPattern","COPY",BODY,{"derivedFrom":makeQuery(id+"F2.opPattern","COPY",BODY,{"derivedFrom":makeQuery(id+"F1.opRevolve","SWEPT_BODY",BODY,{"disambiguationData":[OSD([sQuery(id+"F0.wireOp",EDGE,"E1")])]}),"instanceName":"1"}),"instanceName":"1"}),"instanceName":"1"}),"instanceName":"1"});
            var Q293;
            Q293=makeQuery(id+"F10.opPattern","COPY",BODY,{"derivedFrom":makeQuery(id+"F9.opPattern","COPY",BODY,{"derivedFrom":makeQuery(id+"F4.opPattern","COPY",BODY,{"derivedFrom":makeQuery(id+"F3.opPattern","COPY",BODY,{"derivedFrom":makeQuery(id+"F2.opPattern","COPY",BODY,{"derivedFrom":makeQuery(id+"F1.opRevolve","SWEPT_BODY",BODY,{"disambiguationData":[OSD([sQuery(id+"F0.wireOp",EDGE,"E1")])]}),"instanceName":"1"}),"instanceName":"1"}),"instanceName":"1"}),"instanceName":"1"}),"instanceName":"1"});
            var Q294;
            Q294=makeQuery(id+"F10.opPattern","COPY",BODY,{"derivedFrom":makeQuery(id+"F9.opPattern","COPY",BODY,{"derivedFrom":makeQuery(id+"F5.opPattern","COPY",BODY,{"derivedFrom":makeQuery(id+"F1.opRevolve","SWEPT_BODY",BODY,{"disambiguationData":[OSD([sQuery(id+"F0.wireOp",EDGE,"E1")])]}),"instanceName":"1"}),"instanceName":"1"}),"instanceName":"1"});
            var Q295;
            Q295=makeQuery(id+"F10.opPattern","COPY",BODY,{"derivedFrom":makeQuery(id+"F9.opPattern","COPY",BODY,{"derivedFrom":makeQuery(id+"F5.opPattern","COPY",BODY,{"derivedFrom":makeQuery(id+"F2.opPattern","COPY",BODY,{"derivedFrom":makeQuery(id+"F1.opRevolve","SWEPT_BODY",BODY,{"disambiguationData":[OSD([sQuery(id+"F0.wireOp",EDGE,"E1")])]}),"instanceName":"1"}),"instanceName":"1"}),"instanceName":"1"}),"instanceName":"1"});
            var Q296;
            Q296=makeQuery(id+"F10.opPattern","COPY",BODY,{"derivedFrom":makeQuery(id+"F9.opPattern","COPY",BODY,{"derivedFrom":makeQuery(id+"F5.opPattern","COPY",BODY,{"derivedFrom":makeQuery(id+"F3.opPattern","COPY",BODY,{"derivedFrom":makeQuery(id+"F2.opPattern","COPY",BODY,{"derivedFrom":makeQuery(id+"F1.opRevolve","SWEPT_BODY",BODY,{"disambiguationData":[OSD([sQuery(id+"F0.wireOp",EDGE,"E1")])]}),"instanceName":"1"}),"instanceName":"1"}),"instanceName":"1"}),"instanceName":"1"}),"instanceName":"1"});
            var Q297;
            Q297=makeQuery(id+"F10.opPattern","COPY",BODY,{"derivedFrom":makeQuery(id+"F9.opPattern","COPY",BODY,{"derivedFrom":makeQuery(id+"F5.opPattern","COPY",BODY,{"derivedFrom":makeQuery(id+"F4.opPattern","COPY",BODY,{"derivedFrom":makeQuery(id+"F1.opRevolve","SWEPT_BODY",BODY,{"disambiguationData":[OSD([sQuery(id+"F0.wireOp",EDGE,"E1")])]}),"instanceName":"1"}),"instanceName":"1"}),"instanceName":"1"}),"instanceName":"1"});
            var Q298;
            Q298=makeQuery(id+"F10.opPattern","COPY",BODY,{"derivedFrom":makeQuery(id+"F9.opPattern","COPY",BODY,{"derivedFrom":makeQuery(id+"F5.opPattern","COPY",BODY,{"derivedFrom":makeQuery(id+"F4.opPattern","COPY",BODY,{"derivedFrom":makeQuery(id+"F2.opPattern","COPY",BODY,{"derivedFrom":makeQuery(id+"F1.opRevolve","SWEPT_BODY",BODY,{"disambiguationData":[OSD([sQuery(id+"F0.wireOp",EDGE,"E1")])]}),"instanceName":"1"}),"instanceName":"1"}),"instanceName":"1"}),"instanceName":"1"}),"instanceName":"1"});
            var Q299;
            Q299=makeQuery(id+"F10.opPattern","COPY",BODY,{"derivedFrom":makeQuery(id+"F9.opPattern","COPY",BODY,{"derivedFrom":makeQuery(id+"F5.opPattern","COPY",BODY,{"derivedFrom":makeQuery(id+"F4.opPattern","COPY",BODY,{"derivedFrom":makeQuery(id+"F3.opPattern","COPY",BODY,{"derivedFrom":makeQuery(id+"F2.opPattern","COPY",BODY,{"derivedFrom":makeQuery(id+"F1.opRevolve","SWEPT_BODY",BODY,{"disambiguationData":[OSD([sQuery(id+"F0.wireOp",EDGE,"E1")])]}),"instanceName":"1"}),"instanceName":"1"}),"instanceName":"1"}),"instanceName":"1"}),"instanceName":"1"}),"instanceName":"1"});
            var Q300;
            Q300=makeQuery(id+"F10.opPattern","COPY",BODY,{"derivedFrom":makeQuery(id+"F9.opPattern","COPY",BODY,{"derivedFrom":makeQuery(id+"F6.opPattern","COPY",BODY,{"derivedFrom":makeQuery(id+"F1.opRevolve","SWEPT_BODY",BODY,{"disambiguationData":[OSD([sQuery(id+"F0.wireOp",EDGE,"E1")])]}),"instanceName":"1"}),"instanceName":"1"}),"instanceName":"1"});
            var Q301;
            Q301=makeQuery(id+"F10.opPattern","COPY",BODY,{"derivedFrom":makeQuery(id+"F9.opPattern","COPY",BODY,{"derivedFrom":makeQuery(id+"F6.opPattern","COPY",BODY,{"derivedFrom":makeQuery(id+"F2.opPattern","COPY",BODY,{"derivedFrom":makeQuery(id+"F1.opRevolve","SWEPT_BODY",BODY,{"disambiguationData":[OSD([sQuery(id+"F0.wireOp",EDGE,"E1")])]}),"instanceName":"1"}),"instanceName":"1"}),"instanceName":"1"}),"instanceName":"1"});
            var Q302;
            Q302=makeQuery(id+"F10.opPattern","COPY",BODY,{"derivedFrom":makeQuery(id+"F9.opPattern","COPY",BODY,{"derivedFrom":makeQuery(id+"F6.opPattern","COPY",BODY,{"derivedFrom":makeQuery(id+"F3.opPattern","COPY",BODY,{"derivedFrom":makeQuery(id+"F2.opPattern","COPY",BODY,{"derivedFrom":makeQuery(id+"F1.opRevolve","SWEPT_BODY",BODY,{"disambiguationData":[OSD([sQuery(id+"F0.wireOp",EDGE,"E1")])]}),"instanceName":"1"}),"instanceName":"1"}),"instanceName":"1"}),"instanceName":"1"}),"instanceName":"1"});
            var Q303;
            Q303=makeQuery(id+"F10.opPattern","COPY",BODY,{"derivedFrom":makeQuery(id+"F9.opPattern","COPY",BODY,{"derivedFrom":makeQuery(id+"F6.opPattern","COPY",BODY,{"derivedFrom":makeQuery(id+"F4.opPattern","COPY",BODY,{"derivedFrom":makeQuery(id+"F1.opRevolve","SWEPT_BODY",BODY,{"disambiguationData":[OSD([sQuery(id+"F0.wireOp",EDGE,"E1")])]}),"instanceName":"1"}),"instanceName":"1"}),"instanceName":"1"}),"instanceName":"1"});
            var Q304;
            Q304=makeQuery(id+"F10.opPattern","COPY",BODY,{"derivedFrom":makeQuery(id+"F9.opPattern","COPY",BODY,{"derivedFrom":makeQuery(id+"F6.opPattern","COPY",BODY,{"derivedFrom":makeQuery(id+"F4.opPattern","COPY",BODY,{"derivedFrom":makeQuery(id+"F2.opPattern","COPY",BODY,{"derivedFrom":makeQuery(id+"F1.opRevolve","SWEPT_BODY",BODY,{"disambiguationData":[OSD([sQuery(id+"F0.wireOp",EDGE,"E1")])]}),"instanceName":"1"}),"instanceName":"1"}),"instanceName":"1"}),"instanceName":"1"}),"instanceName":"1"});
            var Q305;
            Q305=makeQuery(id+"F10.opPattern","COPY",BODY,{"derivedFrom":makeQuery(id+"F9.opPattern","COPY",BODY,{"derivedFrom":makeQuery(id+"F6.opPattern","COPY",BODY,{"derivedFrom":makeQuery(id+"F4.opPattern","COPY",BODY,{"derivedFrom":makeQuery(id+"F3.opPattern","COPY",BODY,{"derivedFrom":makeQuery(id+"F2.opPattern","COPY",BODY,{"derivedFrom":makeQuery(id+"F1.opRevolve","SWEPT_BODY",BODY,{"disambiguationData":[OSD([sQuery(id+"F0.wireOp",EDGE,"E1")])]}),"instanceName":"1"}),"instanceName":"1"}),"instanceName":"1"}),"instanceName":"1"}),"instanceName":"1"}),"instanceName":"1"});
            var Q306;
            Q306=makeQuery(id+"F10.opPattern","COPY",BODY,{"derivedFrom":makeQuery(id+"F9.opPattern","COPY",BODY,{"derivedFrom":makeQuery(id+"F6.opPattern","COPY",BODY,{"derivedFrom":makeQuery(id+"F5.opPattern","COPY",BODY,{"derivedFrom":makeQuery(id+"F1.opRevolve","SWEPT_BODY",BODY,{"disambiguationData":[OSD([sQuery(id+"F0.wireOp",EDGE,"E1")])]}),"instanceName":"1"}),"instanceName":"1"}),"instanceName":"1"}),"instanceName":"1"});
            var Q307;
            Q307=makeQuery(id+"F10.opPattern","COPY",BODY,{"derivedFrom":makeQuery(id+"F9.opPattern","COPY",BODY,{"derivedFrom":makeQuery(id+"F6.opPattern","COPY",BODY,{"derivedFrom":makeQuery(id+"F5.opPattern","COPY",BODY,{"derivedFrom":makeQuery(id+"F2.opPattern","COPY",BODY,{"derivedFrom":makeQuery(id+"F1.opRevolve","SWEPT_BODY",BODY,{"disambiguationData":[OSD([sQuery(id+"F0.wireOp",EDGE,"E1")])]}),"instanceName":"1"}),"instanceName":"1"}),"instanceName":"1"}),"instanceName":"1"}),"instanceName":"1"});
            var Q308;
            Q308=makeQuery(id+"F10.opPattern","COPY",BODY,{"derivedFrom":makeQuery(id+"F9.opPattern","COPY",BODY,{"derivedFrom":makeQuery(id+"F6.opPattern","COPY",BODY,{"derivedFrom":makeQuery(id+"F5.opPattern","COPY",BODY,{"derivedFrom":makeQuery(id+"F3.opPattern","COPY",BODY,{"derivedFrom":makeQuery(id+"F2.opPattern","COPY",BODY,{"derivedFrom":makeQuery(id+"F1.opRevolve","SWEPT_BODY",BODY,{"disambiguationData":[OSD([sQuery(id+"F0.wireOp",EDGE,"E1")])]}),"instanceName":"1"}),"instanceName":"1"}),"instanceName":"1"}),"instanceName":"1"}),"instanceName":"1"}),"instanceName":"1"});
            var Q309;
            Q309=makeQuery(id+"F10.opPattern","COPY",BODY,{"derivedFrom":makeQuery(id+"F9.opPattern","COPY",BODY,{"derivedFrom":makeQuery(id+"F6.opPattern","COPY",BODY,{"derivedFrom":makeQuery(id+"F5.opPattern","COPY",BODY,{"derivedFrom":makeQuery(id+"F4.opPattern","COPY",BODY,{"derivedFrom":makeQuery(id+"F1.opRevolve","SWEPT_BODY",BODY,{"disambiguationData":[OSD([sQuery(id+"F0.wireOp",EDGE,"E1")])]}),"instanceName":"1"}),"instanceName":"1"}),"instanceName":"1"}),"instanceName":"1"}),"instanceName":"1"});
            var Q310;
            Q310=makeQuery(id+"F10.opPattern","COPY",BODY,{"derivedFrom":makeQuery(id+"F9.opPattern","COPY",BODY,{"derivedFrom":makeQuery(id+"F6.opPattern","COPY",BODY,{"derivedFrom":makeQuery(id+"F5.opPattern","COPY",BODY,{"derivedFrom":makeQuery(id+"F4.opPattern","COPY",BODY,{"derivedFrom":makeQuery(id+"F2.opPattern","COPY",BODY,{"derivedFrom":makeQuery(id+"F1.opRevolve","SWEPT_BODY",BODY,{"disambiguationData":[OSD([sQuery(id+"F0.wireOp",EDGE,"E1")])]}),"instanceName":"1"}),"instanceName":"1"}),"instanceName":"1"}),"instanceName":"1"}),"instanceName":"1"}),"instanceName":"1"});
            var Q311;
            Q311=makeQuery(id+"F10.opPattern","COPY",BODY,{"derivedFrom":makeQuery(id+"F9.opPattern","COPY",BODY,{"derivedFrom":makeQuery(id+"F6.opPattern","COPY",BODY,{"derivedFrom":makeQuery(id+"F5.opPattern","COPY",BODY,{"derivedFrom":makeQuery(id+"F4.opPattern","COPY",BODY,{"derivedFrom":makeQuery(id+"F3.opPattern","COPY",BODY,{"derivedFrom":makeQuery(id+"F2.opPattern","COPY",BODY,{"derivedFrom":makeQuery(id+"F1.opRevolve","SWEPT_BODY",BODY,{"disambiguationData":[OSD([sQuery(id+"F0.wireOp",EDGE,"E1")])]}),"instanceName":"1"}),"instanceName":"1"}),"instanceName":"1"}),"instanceName":"1"}),"instanceName":"1"}),"instanceName":"1"}),"instanceName":"1"});
            var Q312;
            Q312=makeQuery(id+"F10.opPattern","COPY",BODY,{"derivedFrom":makeQuery(id+"F9.opPattern","COPY",BODY,{"derivedFrom":makeQuery(id+"F7.opPattern","COPY",BODY,{"derivedFrom":makeQuery(id+"F1.opRevolve","SWEPT_BODY",BODY,{"disambiguationData":[OSD([sQuery(id+"F0.wireOp",EDGE,"E1")])]}),"instanceName":"1"}),"instanceName":"1"}),"instanceName":"1"});
            var Q313;
            Q313=makeQuery(id+"F10.opPattern","COPY",BODY,{"derivedFrom":makeQuery(id+"F9.opPattern","COPY",BODY,{"derivedFrom":makeQuery(id+"F7.opPattern","COPY",BODY,{"derivedFrom":makeQuery(id+"F2.opPattern","COPY",BODY,{"derivedFrom":makeQuery(id+"F1.opRevolve","SWEPT_BODY",BODY,{"disambiguationData":[OSD([sQuery(id+"F0.wireOp",EDGE,"E1")])]}),"instanceName":"1"}),"instanceName":"1"}),"instanceName":"1"}),"instanceName":"1"});
            var Q314;
            Q314=makeQuery(id+"F10.opPattern","COPY",BODY,{"derivedFrom":makeQuery(id+"F9.opPattern","COPY",BODY,{"derivedFrom":makeQuery(id+"F7.opPattern","COPY",BODY,{"derivedFrom":makeQuery(id+"F3.opPattern","COPY",BODY,{"derivedFrom":makeQuery(id+"F2.opPattern","COPY",BODY,{"derivedFrom":makeQuery(id+"F1.opRevolve","SWEPT_BODY",BODY,{"disambiguationData":[OSD([sQuery(id+"F0.wireOp",EDGE,"E1")])]}),"instanceName":"1"}),"instanceName":"1"}),"instanceName":"1"}),"instanceName":"1"}),"instanceName":"1"});
            var Q315;
            Q315=makeQuery(id+"F10.opPattern","COPY",BODY,{"derivedFrom":makeQuery(id+"F9.opPattern","COPY",BODY,{"derivedFrom":makeQuery(id+"F7.opPattern","COPY",BODY,{"derivedFrom":makeQuery(id+"F4.opPattern","COPY",BODY,{"derivedFrom":makeQuery(id+"F1.opRevolve","SWEPT_BODY",BODY,{"disambiguationData":[OSD([sQuery(id+"F0.wireOp",EDGE,"E1")])]}),"instanceName":"1"}),"instanceName":"1"}),"instanceName":"1"}),"instanceName":"1"});
            var Q316;
            Q316=makeQuery(id+"F10.opPattern","COPY",BODY,{"derivedFrom":makeQuery(id+"F9.opPattern","COPY",BODY,{"derivedFrom":makeQuery(id+"F7.opPattern","COPY",BODY,{"derivedFrom":makeQuery(id+"F4.opPattern","COPY",BODY,{"derivedFrom":makeQuery(id+"F2.opPattern","COPY",BODY,{"derivedFrom":makeQuery(id+"F1.opRevolve","SWEPT_BODY",BODY,{"disambiguationData":[OSD([sQuery(id+"F0.wireOp",EDGE,"E1")])]}),"instanceName":"1"}),"instanceName":"1"}),"instanceName":"1"}),"instanceName":"1"}),"instanceName":"1"});
            var Q317;
            Q317=makeQuery(id+"F10.opPattern","COPY",BODY,{"derivedFrom":makeQuery(id+"F9.opPattern","COPY",BODY,{"derivedFrom":makeQuery(id+"F7.opPattern","COPY",BODY,{"derivedFrom":makeQuery(id+"F4.opPattern","COPY",BODY,{"derivedFrom":makeQuery(id+"F3.opPattern","COPY",BODY,{"derivedFrom":makeQuery(id+"F2.opPattern","COPY",BODY,{"derivedFrom":makeQuery(id+"F1.opRevolve","SWEPT_BODY",BODY,{"disambiguationData":[OSD([sQuery(id+"F0.wireOp",EDGE,"E1")])]}),"instanceName":"1"}),"instanceName":"1"}),"instanceName":"1"}),"instanceName":"1"}),"instanceName":"1"}),"instanceName":"1"});
            var Q318;
            Q318=makeQuery(id+"F10.opPattern","COPY",BODY,{"derivedFrom":makeQuery(id+"F9.opPattern","COPY",BODY,{"derivedFrom":makeQuery(id+"F7.opPattern","COPY",BODY,{"derivedFrom":makeQuery(id+"F5.opPattern","COPY",BODY,{"derivedFrom":makeQuery(id+"F1.opRevolve","SWEPT_BODY",BODY,{"disambiguationData":[OSD([sQuery(id+"F0.wireOp",EDGE,"E1")])]}),"instanceName":"1"}),"instanceName":"1"}),"instanceName":"1"}),"instanceName":"1"});
            var Q319;
            Q319=makeQuery(id+"F10.opPattern","COPY",BODY,{"derivedFrom":makeQuery(id+"F9.opPattern","COPY",BODY,{"derivedFrom":makeQuery(id+"F7.opPattern","COPY",BODY,{"derivedFrom":makeQuery(id+"F5.opPattern","COPY",BODY,{"derivedFrom":makeQuery(id+"F2.opPattern","COPY",BODY,{"derivedFrom":makeQuery(id+"F1.opRevolve","SWEPT_BODY",BODY,{"disambiguationData":[OSD([sQuery(id+"F0.wireOp",EDGE,"E1")])]}),"instanceName":"1"}),"instanceName":"1"}),"instanceName":"1"}),"instanceName":"1"}),"instanceName":"1"});
            var Q320;
            Q320=makeQuery(id+"F10.opPattern","COPY",BODY,{"derivedFrom":makeQuery(id+"F9.opPattern","COPY",BODY,{"derivedFrom":makeQuery(id+"F7.opPattern","COPY",BODY,{"derivedFrom":makeQuery(id+"F5.opPattern","COPY",BODY,{"derivedFrom":makeQuery(id+"F3.opPattern","COPY",BODY,{"derivedFrom":makeQuery(id+"F2.opPattern","COPY",BODY,{"derivedFrom":makeQuery(id+"F1.opRevolve","SWEPT_BODY",BODY,{"disambiguationData":[OSD([sQuery(id+"F0.wireOp",EDGE,"E1")])]}),"instanceName":"1"}),"instanceName":"1"}),"instanceName":"1"}),"instanceName":"1"}),"instanceName":"1"}),"instanceName":"1"});
            var Q321;
            Q321=makeQuery(id+"F10.opPattern","COPY",BODY,{"derivedFrom":makeQuery(id+"F9.opPattern","COPY",BODY,{"derivedFrom":makeQuery(id+"F7.opPattern","COPY",BODY,{"derivedFrom":makeQuery(id+"F5.opPattern","COPY",BODY,{"derivedFrom":makeQuery(id+"F4.opPattern","COPY",BODY,{"derivedFrom":makeQuery(id+"F1.opRevolve","SWEPT_BODY",BODY,{"disambiguationData":[OSD([sQuery(id+"F0.wireOp",EDGE,"E1")])]}),"instanceName":"1"}),"instanceName":"1"}),"instanceName":"1"}),"instanceName":"1"}),"instanceName":"1"});
            var Q322;
            Q322=makeQuery(id+"F10.opPattern","COPY",BODY,{"derivedFrom":makeQuery(id+"F9.opPattern","COPY",BODY,{"derivedFrom":makeQuery(id+"F7.opPattern","COPY",BODY,{"derivedFrom":makeQuery(id+"F5.opPattern","COPY",BODY,{"derivedFrom":makeQuery(id+"F4.opPattern","COPY",BODY,{"derivedFrom":makeQuery(id+"F2.opPattern","COPY",BODY,{"derivedFrom":makeQuery(id+"F1.opRevolve","SWEPT_BODY",BODY,{"disambiguationData":[OSD([sQuery(id+"F0.wireOp",EDGE,"E1")])]}),"instanceName":"1"}),"instanceName":"1"}),"instanceName":"1"}),"instanceName":"1"}),"instanceName":"1"}),"instanceName":"1"});
            var Q323;
            Q323=makeQuery(id+"F10.opPattern","COPY",BODY,{"derivedFrom":makeQuery(id+"F9.opPattern","COPY",BODY,{"derivedFrom":makeQuery(id+"F7.opPattern","COPY",BODY,{"derivedFrom":makeQuery(id+"F5.opPattern","COPY",BODY,{"derivedFrom":makeQuery(id+"F4.opPattern","COPY",BODY,{"derivedFrom":makeQuery(id+"F3.opPattern","COPY",BODY,{"derivedFrom":makeQuery(id+"F2.opPattern","COPY",BODY,{"derivedFrom":makeQuery(id+"F1.opRevolve","SWEPT_BODY",BODY,{"disambiguationData":[OSD([sQuery(id+"F0.wireOp",EDGE,"E1")])]}),"instanceName":"1"}),"instanceName":"1"}),"instanceName":"1"}),"instanceName":"1"}),"instanceName":"1"}),"instanceName":"1"}),"instanceName":"1"});
            var Q324;
            Q324=makeQuery(id+"F10.opPattern","COPY",BODY,{"derivedFrom":makeQuery(id+"F9.opPattern","COPY",BODY,{"derivedFrom":makeQuery(id+"F7.opPattern","COPY",BODY,{"derivedFrom":makeQuery(id+"F6.opPattern","COPY",BODY,{"derivedFrom":makeQuery(id+"F1.opRevolve","SWEPT_BODY",BODY,{"disambiguationData":[OSD([sQuery(id+"F0.wireOp",EDGE,"E1")])]}),"instanceName":"1"}),"instanceName":"1"}),"instanceName":"1"}),"instanceName":"1"});
            var Q325;
            Q325=makeQuery(id+"F10.opPattern","COPY",BODY,{"derivedFrom":makeQuery(id+"F9.opPattern","COPY",BODY,{"derivedFrom":makeQuery(id+"F7.opPattern","COPY",BODY,{"derivedFrom":makeQuery(id+"F6.opPattern","COPY",BODY,{"derivedFrom":makeQuery(id+"F2.opPattern","COPY",BODY,{"derivedFrom":makeQuery(id+"F1.opRevolve","SWEPT_BODY",BODY,{"disambiguationData":[OSD([sQuery(id+"F0.wireOp",EDGE,"E1")])]}),"instanceName":"1"}),"instanceName":"1"}),"instanceName":"1"}),"instanceName":"1"}),"instanceName":"1"});
            var Q326;
            Q326=makeQuery(id+"F10.opPattern","COPY",BODY,{"derivedFrom":makeQuery(id+"F9.opPattern","COPY",BODY,{"derivedFrom":makeQuery(id+"F7.opPattern","COPY",BODY,{"derivedFrom":makeQuery(id+"F6.opPattern","COPY",BODY,{"derivedFrom":makeQuery(id+"F3.opPattern","COPY",BODY,{"derivedFrom":makeQuery(id+"F2.opPattern","COPY",BODY,{"derivedFrom":makeQuery(id+"F1.opRevolve","SWEPT_BODY",BODY,{"disambiguationData":[OSD([sQuery(id+"F0.wireOp",EDGE,"E1")])]}),"instanceName":"1"}),"instanceName":"1"}),"instanceName":"1"}),"instanceName":"1"}),"instanceName":"1"}),"instanceName":"1"});
            var Q327;
            Q327=makeQuery(id+"F10.opPattern","COPY",BODY,{"derivedFrom":makeQuery(id+"F9.opPattern","COPY",BODY,{"derivedFrom":makeQuery(id+"F7.opPattern","COPY",BODY,{"derivedFrom":makeQuery(id+"F6.opPattern","COPY",BODY,{"derivedFrom":makeQuery(id+"F4.opPattern","COPY",BODY,{"derivedFrom":makeQuery(id+"F1.opRevolve","SWEPT_BODY",BODY,{"disambiguationData":[OSD([sQuery(id+"F0.wireOp",EDGE,"E1")])]}),"instanceName":"1"}),"instanceName":"1"}),"instanceName":"1"}),"instanceName":"1"}),"instanceName":"1"});
            var Q328;
            Q328=makeQuery(id+"F10.opPattern","COPY",BODY,{"derivedFrom":makeQuery(id+"F9.opPattern","COPY",BODY,{"derivedFrom":makeQuery(id+"F7.opPattern","COPY",BODY,{"derivedFrom":makeQuery(id+"F6.opPattern","COPY",BODY,{"derivedFrom":makeQuery(id+"F4.opPattern","COPY",BODY,{"derivedFrom":makeQuery(id+"F2.opPattern","COPY",BODY,{"derivedFrom":makeQuery(id+"F1.opRevolve","SWEPT_BODY",BODY,{"disambiguationData":[OSD([sQuery(id+"F0.wireOp",EDGE,"E1")])]}),"instanceName":"1"}),"instanceName":"1"}),"instanceName":"1"}),"instanceName":"1"}),"instanceName":"1"}),"instanceName":"1"});
            var Q329;
            Q329=makeQuery(id+"F10.opPattern","COPY",BODY,{"derivedFrom":makeQuery(id+"F9.opPattern","COPY",BODY,{"derivedFrom":makeQuery(id+"F7.opPattern","COPY",BODY,{"derivedFrom":makeQuery(id+"F6.opPattern","COPY",BODY,{"derivedFrom":makeQuery(id+"F4.opPattern","COPY",BODY,{"derivedFrom":makeQuery(id+"F3.opPattern","COPY",BODY,{"derivedFrom":makeQuery(id+"F2.opPattern","COPY",BODY,{"derivedFrom":makeQuery(id+"F1.opRevolve","SWEPT_BODY",BODY,{"disambiguationData":[OSD([sQuery(id+"F0.wireOp",EDGE,"E1")])]}),"instanceName":"1"}),"instanceName":"1"}),"instanceName":"1"}),"instanceName":"1"}),"instanceName":"1"}),"instanceName":"1"}),"instanceName":"1"});
            var Q330;
            Q330=makeQuery(id+"F10.opPattern","COPY",BODY,{"derivedFrom":makeQuery(id+"F9.opPattern","COPY",BODY,{"derivedFrom":makeQuery(id+"F7.opPattern","COPY",BODY,{"derivedFrom":makeQuery(id+"F6.opPattern","COPY",BODY,{"derivedFrom":makeQuery(id+"F5.opPattern","COPY",BODY,{"derivedFrom":makeQuery(id+"F1.opRevolve","SWEPT_BODY",BODY,{"disambiguationData":[OSD([sQuery(id+"F0.wireOp",EDGE,"E1")])]}),"instanceName":"1"}),"instanceName":"1"}),"instanceName":"1"}),"instanceName":"1"}),"instanceName":"1"});
            var Q331;
            Q331=makeQuery(id+"F10.opPattern","COPY",BODY,{"derivedFrom":makeQuery(id+"F9.opPattern","COPY",BODY,{"derivedFrom":makeQuery(id+"F7.opPattern","COPY",BODY,{"derivedFrom":makeQuery(id+"F6.opPattern","COPY",BODY,{"derivedFrom":makeQuery(id+"F5.opPattern","COPY",BODY,{"derivedFrom":makeQuery(id+"F2.opPattern","COPY",BODY,{"derivedFrom":makeQuery(id+"F1.opRevolve","SWEPT_BODY",BODY,{"disambiguationData":[OSD([sQuery(id+"F0.wireOp",EDGE,"E1")])]}),"instanceName":"1"}),"instanceName":"1"}),"instanceName":"1"}),"instanceName":"1"}),"instanceName":"1"}),"instanceName":"1"});
            var Q332;
            Q332=makeQuery(id+"F10.opPattern","COPY",BODY,{"derivedFrom":makeQuery(id+"F9.opPattern","COPY",BODY,{"derivedFrom":makeQuery(id+"F7.opPattern","COPY",BODY,{"derivedFrom":makeQuery(id+"F6.opPattern","COPY",BODY,{"derivedFrom":makeQuery(id+"F5.opPattern","COPY",BODY,{"derivedFrom":makeQuery(id+"F3.opPattern","COPY",BODY,{"derivedFrom":makeQuery(id+"F2.opPattern","COPY",BODY,{"derivedFrom":makeQuery(id+"F1.opRevolve","SWEPT_BODY",BODY,{"disambiguationData":[OSD([sQuery(id+"F0.wireOp",EDGE,"E1")])]}),"instanceName":"1"}),"instanceName":"1"}),"instanceName":"1"}),"instanceName":"1"}),"instanceName":"1"}),"instanceName":"1"}),"instanceName":"1"});
            var Q333;
            Q333=makeQuery(id+"F10.opPattern","COPY",BODY,{"derivedFrom":makeQuery(id+"F9.opPattern","COPY",BODY,{"derivedFrom":makeQuery(id+"F7.opPattern","COPY",BODY,{"derivedFrom":makeQuery(id+"F6.opPattern","COPY",BODY,{"derivedFrom":makeQuery(id+"F5.opPattern","COPY",BODY,{"derivedFrom":makeQuery(id+"F4.opPattern","COPY",BODY,{"derivedFrom":makeQuery(id+"F1.opRevolve","SWEPT_BODY",BODY,{"disambiguationData":[OSD([sQuery(id+"F0.wireOp",EDGE,"E1")])]}),"instanceName":"1"}),"instanceName":"1"}),"instanceName":"1"}),"instanceName":"1"}),"instanceName":"1"}),"instanceName":"1"});
            var Q334;
            Q334=makeQuery(id+"F10.opPattern","COPY",BODY,{"derivedFrom":makeQuery(id+"F9.opPattern","COPY",BODY,{"derivedFrom":makeQuery(id+"F7.opPattern","COPY",BODY,{"derivedFrom":makeQuery(id+"F6.opPattern","COPY",BODY,{"derivedFrom":makeQuery(id+"F5.opPattern","COPY",BODY,{"derivedFrom":makeQuery(id+"F4.opPattern","COPY",BODY,{"derivedFrom":makeQuery(id+"F2.opPattern","COPY",BODY,{"derivedFrom":makeQuery(id+"F1.opRevolve","SWEPT_BODY",BODY,{"disambiguationData":[OSD([sQuery(id+"F0.wireOp",EDGE,"E1")])]}),"instanceName":"1"}),"instanceName":"1"}),"instanceName":"1"}),"instanceName":"1"}),"instanceName":"1"}),"instanceName":"1"}),"instanceName":"1"});
            var Q335;
            Q335=makeQuery(id+"F10.opPattern","COPY",BODY,{"derivedFrom":makeQuery(id+"F9.opPattern","COPY",BODY,{"derivedFrom":makeQuery(id+"F7.opPattern","COPY",BODY,{"derivedFrom":makeQuery(id+"F6.opPattern","COPY",BODY,{"derivedFrom":makeQuery(id+"F5.opPattern","COPY",BODY,{"derivedFrom":makeQuery(id+"F4.opPattern","COPY",BODY,{"derivedFrom":makeQuery(id+"F3.opPattern","COPY",BODY,{"derivedFrom":makeQuery(id+"F2.opPattern","COPY",BODY,{"derivedFrom":makeQuery(id+"F1.opRevolve","SWEPT_BODY",BODY,{"disambiguationData":[OSD([sQuery(id+"F0.wireOp",EDGE,"E1")])]}),"instanceName":"1"}),"instanceName":"1"}),"instanceName":"1"}),"instanceName":"1"}),"instanceName":"1"}),"instanceName":"1"}),"instanceName":"1"}),"instanceName":"1"});
            var Q336;
            Q336=makeQuery(id+"F10.opPattern","COPY",BODY,{"derivedFrom":makeQuery(id+"F9.opPattern","COPY",BODY,{"derivedFrom":makeQuery(id+"F8.opPattern","COPY",BODY,{"derivedFrom":makeQuery(id+"F1.opRevolve","SWEPT_BODY",BODY,{"disambiguationData":[OSD([sQuery(id+"F0.wireOp",EDGE,"E1")])]}),"instanceName":"1"}),"instanceName":"1"}),"instanceName":"1"});
            var Q337;
            Q337=makeQuery(id+"F10.opPattern","COPY",BODY,{"derivedFrom":makeQuery(id+"F9.opPattern","COPY",BODY,{"derivedFrom":makeQuery(id+"F8.opPattern","COPY",BODY,{"derivedFrom":makeQuery(id+"F2.opPattern","COPY",BODY,{"derivedFrom":makeQuery(id+"F1.opRevolve","SWEPT_BODY",BODY,{"disambiguationData":[OSD([sQuery(id+"F0.wireOp",EDGE,"E1")])]}),"instanceName":"1"}),"instanceName":"1"}),"instanceName":"1"}),"instanceName":"1"});
            var Q338;
            Q338=makeQuery(id+"F10.opPattern","COPY",BODY,{"derivedFrom":makeQuery(id+"F9.opPattern","COPY",BODY,{"derivedFrom":makeQuery(id+"F8.opPattern","COPY",BODY,{"derivedFrom":makeQuery(id+"F3.opPattern","COPY",BODY,{"derivedFrom":makeQuery(id+"F2.opPattern","COPY",BODY,{"derivedFrom":makeQuery(id+"F1.opRevolve","SWEPT_BODY",BODY,{"disambiguationData":[OSD([sQuery(id+"F0.wireOp",EDGE,"E1")])]}),"instanceName":"1"}),"instanceName":"1"}),"instanceName":"1"}),"instanceName":"1"}),"instanceName":"1"});
            var Q339;
            Q339=makeQuery(id+"F10.opPattern","COPY",BODY,{"derivedFrom":makeQuery(id+"F9.opPattern","COPY",BODY,{"derivedFrom":makeQuery(id+"F8.opPattern","COPY",BODY,{"derivedFrom":makeQuery(id+"F4.opPattern","COPY",BODY,{"derivedFrom":makeQuery(id+"F1.opRevolve","SWEPT_BODY",BODY,{"disambiguationData":[OSD([sQuery(id+"F0.wireOp",EDGE,"E1")])]}),"instanceName":"1"}),"instanceName":"1"}),"instanceName":"1"}),"instanceName":"1"});
            var Q340;
            Q340=makeQuery(id+"F10.opPattern","COPY",BODY,{"derivedFrom":makeQuery(id+"F9.opPattern","COPY",BODY,{"derivedFrom":makeQuery(id+"F8.opPattern","COPY",BODY,{"derivedFrom":makeQuery(id+"F4.opPattern","COPY",BODY,{"derivedFrom":makeQuery(id+"F2.opPattern","COPY",BODY,{"derivedFrom":makeQuery(id+"F1.opRevolve","SWEPT_BODY",BODY,{"disambiguationData":[OSD([sQuery(id+"F0.wireOp",EDGE,"E1")])]}),"instanceName":"1"}),"instanceName":"1"}),"instanceName":"1"}),"instanceName":"1"}),"instanceName":"1"});
            var Q341;
            Q341=makeQuery(id+"F10.opPattern","COPY",BODY,{"derivedFrom":makeQuery(id+"F9.opPattern","COPY",BODY,{"derivedFrom":makeQuery(id+"F8.opPattern","COPY",BODY,{"derivedFrom":makeQuery(id+"F4.opPattern","COPY",BODY,{"derivedFrom":makeQuery(id+"F3.opPattern","COPY",BODY,{"derivedFrom":makeQuery(id+"F2.opPattern","COPY",BODY,{"derivedFrom":makeQuery(id+"F1.opRevolve","SWEPT_BODY",BODY,{"disambiguationData":[OSD([sQuery(id+"F0.wireOp",EDGE,"E1")])]}),"instanceName":"1"}),"instanceName":"1"}),"instanceName":"1"}),"instanceName":"1"}),"instanceName":"1"}),"instanceName":"1"});
            var Q342;
            Q342=makeQuery(id+"F10.opPattern","COPY",BODY,{"derivedFrom":makeQuery(id+"F9.opPattern","COPY",BODY,{"derivedFrom":makeQuery(id+"F8.opPattern","COPY",BODY,{"derivedFrom":makeQuery(id+"F5.opPattern","COPY",BODY,{"derivedFrom":makeQuery(id+"F1.opRevolve","SWEPT_BODY",BODY,{"disambiguationData":[OSD([sQuery(id+"F0.wireOp",EDGE,"E1")])]}),"instanceName":"1"}),"instanceName":"1"}),"instanceName":"1"}),"instanceName":"1"});
            var Q343;
            Q343=makeQuery(id+"F10.opPattern","COPY",BODY,{"derivedFrom":makeQuery(id+"F9.opPattern","COPY",BODY,{"derivedFrom":makeQuery(id+"F8.opPattern","COPY",BODY,{"derivedFrom":makeQuery(id+"F5.opPattern","COPY",BODY,{"derivedFrom":makeQuery(id+"F2.opPattern","COPY",BODY,{"derivedFrom":makeQuery(id+"F1.opRevolve","SWEPT_BODY",BODY,{"disambiguationData":[OSD([sQuery(id+"F0.wireOp",EDGE,"E1")])]}),"instanceName":"1"}),"instanceName":"1"}),"instanceName":"1"}),"instanceName":"1"}),"instanceName":"1"});
            var Q344;
            Q344=makeQuery(id+"F10.opPattern","COPY",BODY,{"derivedFrom":makeQuery(id+"F9.opPattern","COPY",BODY,{"derivedFrom":makeQuery(id+"F8.opPattern","COPY",BODY,{"derivedFrom":makeQuery(id+"F5.opPattern","COPY",BODY,{"derivedFrom":makeQuery(id+"F3.opPattern","COPY",BODY,{"derivedFrom":makeQuery(id+"F2.opPattern","COPY",BODY,{"derivedFrom":makeQuery(id+"F1.opRevolve","SWEPT_BODY",BODY,{"disambiguationData":[OSD([sQuery(id+"F0.wireOp",EDGE,"E1")])]}),"instanceName":"1"}),"instanceName":"1"}),"instanceName":"1"}),"instanceName":"1"}),"instanceName":"1"}),"instanceName":"1"});
            var Q345;
            Q345=makeQuery(id+"F10.opPattern","COPY",BODY,{"derivedFrom":makeQuery(id+"F9.opPattern","COPY",BODY,{"derivedFrom":makeQuery(id+"F8.opPattern","COPY",BODY,{"derivedFrom":makeQuery(id+"F5.opPattern","COPY",BODY,{"derivedFrom":makeQuery(id+"F4.opPattern","COPY",BODY,{"derivedFrom":makeQuery(id+"F1.opRevolve","SWEPT_BODY",BODY,{"disambiguationData":[OSD([sQuery(id+"F0.wireOp",EDGE,"E1")])]}),"instanceName":"1"}),"instanceName":"1"}),"instanceName":"1"}),"instanceName":"1"}),"instanceName":"1"});
            var Q346;
            Q346=makeQuery(id+"F10.opPattern","COPY",BODY,{"derivedFrom":makeQuery(id+"F9.opPattern","COPY",BODY,{"derivedFrom":makeQuery(id+"F8.opPattern","COPY",BODY,{"derivedFrom":makeQuery(id+"F5.opPattern","COPY",BODY,{"derivedFrom":makeQuery(id+"F4.opPattern","COPY",BODY,{"derivedFrom":makeQuery(id+"F2.opPattern","COPY",BODY,{"derivedFrom":makeQuery(id+"F1.opRevolve","SWEPT_BODY",BODY,{"disambiguationData":[OSD([sQuery(id+"F0.wireOp",EDGE,"E1")])]}),"instanceName":"1"}),"instanceName":"1"}),"instanceName":"1"}),"instanceName":"1"}),"instanceName":"1"}),"instanceName":"1"});
            var Q347;
            Q347=makeQuery(id+"F10.opPattern","COPY",BODY,{"derivedFrom":makeQuery(id+"F9.opPattern","COPY",BODY,{"derivedFrom":makeQuery(id+"F8.opPattern","COPY",BODY,{"derivedFrom":makeQuery(id+"F5.opPattern","COPY",BODY,{"derivedFrom":makeQuery(id+"F4.opPattern","COPY",BODY,{"derivedFrom":makeQuery(id+"F3.opPattern","COPY",BODY,{"derivedFrom":makeQuery(id+"F2.opPattern","COPY",BODY,{"derivedFrom":makeQuery(id+"F1.opRevolve","SWEPT_BODY",BODY,{"disambiguationData":[OSD([sQuery(id+"F0.wireOp",EDGE,"E1")])]}),"instanceName":"1"}),"instanceName":"1"}),"instanceName":"1"}),"instanceName":"1"}),"instanceName":"1"}),"instanceName":"1"}),"instanceName":"1"});
            var Q348;
            Q348=makeQuery(id+"F10.opPattern","COPY",BODY,{"derivedFrom":makeQuery(id+"F9.opPattern","COPY",BODY,{"derivedFrom":makeQuery(id+"F8.opPattern","COPY",BODY,{"derivedFrom":makeQuery(id+"F6.opPattern","COPY",BODY,{"derivedFrom":makeQuery(id+"F1.opRevolve","SWEPT_BODY",BODY,{"disambiguationData":[OSD([sQuery(id+"F0.wireOp",EDGE,"E1")])]}),"instanceName":"1"}),"instanceName":"1"}),"instanceName":"1"}),"instanceName":"1"});
            var Q349;
            Q349=makeQuery(id+"F10.opPattern","COPY",BODY,{"derivedFrom":makeQuery(id+"F9.opPattern","COPY",BODY,{"derivedFrom":makeQuery(id+"F8.opPattern","COPY",BODY,{"derivedFrom":makeQuery(id+"F6.opPattern","COPY",BODY,{"derivedFrom":makeQuery(id+"F2.opPattern","COPY",BODY,{"derivedFrom":makeQuery(id+"F1.opRevolve","SWEPT_BODY",BODY,{"disambiguationData":[OSD([sQuery(id+"F0.wireOp",EDGE,"E1")])]}),"instanceName":"1"}),"instanceName":"1"}),"instanceName":"1"}),"instanceName":"1"}),"instanceName":"1"});
            var Q350;
            Q350=makeQuery(id+"F10.opPattern","COPY",BODY,{"derivedFrom":makeQuery(id+"F9.opPattern","COPY",BODY,{"derivedFrom":makeQuery(id+"F8.opPattern","COPY",BODY,{"derivedFrom":makeQuery(id+"F6.opPattern","COPY",BODY,{"derivedFrom":makeQuery(id+"F3.opPattern","COPY",BODY,{"derivedFrom":makeQuery(id+"F2.opPattern","COPY",BODY,{"derivedFrom":makeQuery(id+"F1.opRevolve","SWEPT_BODY",BODY,{"disambiguationData":[OSD([sQuery(id+"F0.wireOp",EDGE,"E1")])]}),"instanceName":"1"}),"instanceName":"1"}),"instanceName":"1"}),"instanceName":"1"}),"instanceName":"1"}),"instanceName":"1"});
            var Q351;
            Q351=makeQuery(id+"F10.opPattern","COPY",BODY,{"derivedFrom":makeQuery(id+"F9.opPattern","COPY",BODY,{"derivedFrom":makeQuery(id+"F8.opPattern","COPY",BODY,{"derivedFrom":makeQuery(id+"F6.opPattern","COPY",BODY,{"derivedFrom":makeQuery(id+"F4.opPattern","COPY",BODY,{"derivedFrom":makeQuery(id+"F1.opRevolve","SWEPT_BODY",BODY,{"disambiguationData":[OSD([sQuery(id+"F0.wireOp",EDGE,"E1")])]}),"instanceName":"1"}),"instanceName":"1"}),"instanceName":"1"}),"instanceName":"1"}),"instanceName":"1"});
            var Q352;
            Q352=makeQuery(id+"F10.opPattern","COPY",BODY,{"derivedFrom":makeQuery(id+"F9.opPattern","COPY",BODY,{"derivedFrom":makeQuery(id+"F8.opPattern","COPY",BODY,{"derivedFrom":makeQuery(id+"F6.opPattern","COPY",BODY,{"derivedFrom":makeQuery(id+"F4.opPattern","COPY",BODY,{"derivedFrom":makeQuery(id+"F2.opPattern","COPY",BODY,{"derivedFrom":makeQuery(id+"F1.opRevolve","SWEPT_BODY",BODY,{"disambiguationData":[OSD([sQuery(id+"F0.wireOp",EDGE,"E1")])]}),"instanceName":"1"}),"instanceName":"1"}),"instanceName":"1"}),"instanceName":"1"}),"instanceName":"1"}),"instanceName":"1"});
            var Q353;
            Q353=makeQuery(id+"F10.opPattern","COPY",BODY,{"derivedFrom":makeQuery(id+"F9.opPattern","COPY",BODY,{"derivedFrom":makeQuery(id+"F8.opPattern","COPY",BODY,{"derivedFrom":makeQuery(id+"F6.opPattern","COPY",BODY,{"derivedFrom":makeQuery(id+"F4.opPattern","COPY",BODY,{"derivedFrom":makeQuery(id+"F3.opPattern","COPY",BODY,{"derivedFrom":makeQuery(id+"F2.opPattern","COPY",BODY,{"derivedFrom":makeQuery(id+"F1.opRevolve","SWEPT_BODY",BODY,{"disambiguationData":[OSD([sQuery(id+"F0.wireOp",EDGE,"E1")])]}),"instanceName":"1"}),"instanceName":"1"}),"instanceName":"1"}),"instanceName":"1"}),"instanceName":"1"}),"instanceName":"1"}),"instanceName":"1"});
            var Q354;
            Q354=makeQuery(id+"F10.opPattern","COPY",BODY,{"derivedFrom":makeQuery(id+"F9.opPattern","COPY",BODY,{"derivedFrom":makeQuery(id+"F8.opPattern","COPY",BODY,{"derivedFrom":makeQuery(id+"F6.opPattern","COPY",BODY,{"derivedFrom":makeQuery(id+"F5.opPattern","COPY",BODY,{"derivedFrom":makeQuery(id+"F1.opRevolve","SWEPT_BODY",BODY,{"disambiguationData":[OSD([sQuery(id+"F0.wireOp",EDGE,"E1")])]}),"instanceName":"1"}),"instanceName":"1"}),"instanceName":"1"}),"instanceName":"1"}),"instanceName":"1"});
            var Q355;
            Q355=makeQuery(id+"F10.opPattern","COPY",BODY,{"derivedFrom":makeQuery(id+"F9.opPattern","COPY",BODY,{"derivedFrom":makeQuery(id+"F8.opPattern","COPY",BODY,{"derivedFrom":makeQuery(id+"F6.opPattern","COPY",BODY,{"derivedFrom":makeQuery(id+"F5.opPattern","COPY",BODY,{"derivedFrom":makeQuery(id+"F2.opPattern","COPY",BODY,{"derivedFrom":makeQuery(id+"F1.opRevolve","SWEPT_BODY",BODY,{"disambiguationData":[OSD([sQuery(id+"F0.wireOp",EDGE,"E1")])]}),"instanceName":"1"}),"instanceName":"1"}),"instanceName":"1"}),"instanceName":"1"}),"instanceName":"1"}),"instanceName":"1"});
            var Q356;
            Q356=makeQuery(id+"F10.opPattern","COPY",BODY,{"derivedFrom":makeQuery(id+"F9.opPattern","COPY",BODY,{"derivedFrom":makeQuery(id+"F8.opPattern","COPY",BODY,{"derivedFrom":makeQuery(id+"F6.opPattern","COPY",BODY,{"derivedFrom":makeQuery(id+"F5.opPattern","COPY",BODY,{"derivedFrom":makeQuery(id+"F3.opPattern","COPY",BODY,{"derivedFrom":makeQuery(id+"F2.opPattern","COPY",BODY,{"derivedFrom":makeQuery(id+"F1.opRevolve","SWEPT_BODY",BODY,{"disambiguationData":[OSD([sQuery(id+"F0.wireOp",EDGE,"E1")])]}),"instanceName":"1"}),"instanceName":"1"}),"instanceName":"1"}),"instanceName":"1"}),"instanceName":"1"}),"instanceName":"1"}),"instanceName":"1"});
            var Q357;
            Q357=makeQuery(id+"F10.opPattern","COPY",BODY,{"derivedFrom":makeQuery(id+"F9.opPattern","COPY",BODY,{"derivedFrom":makeQuery(id+"F8.opPattern","COPY",BODY,{"derivedFrom":makeQuery(id+"F6.opPattern","COPY",BODY,{"derivedFrom":makeQuery(id+"F5.opPattern","COPY",BODY,{"derivedFrom":makeQuery(id+"F4.opPattern","COPY",BODY,{"derivedFrom":makeQuery(id+"F1.opRevolve","SWEPT_BODY",BODY,{"disambiguationData":[OSD([sQuery(id+"F0.wireOp",EDGE,"E1")])]}),"instanceName":"1"}),"instanceName":"1"}),"instanceName":"1"}),"instanceName":"1"}),"instanceName":"1"}),"instanceName":"1"});
            var Q358;
            Q358=makeQuery(id+"F10.opPattern","COPY",BODY,{"derivedFrom":makeQuery(id+"F9.opPattern","COPY",BODY,{"derivedFrom":makeQuery(id+"F8.opPattern","COPY",BODY,{"derivedFrom":makeQuery(id+"F6.opPattern","COPY",BODY,{"derivedFrom":makeQuery(id+"F5.opPattern","COPY",BODY,{"derivedFrom":makeQuery(id+"F4.opPattern","COPY",BODY,{"derivedFrom":makeQuery(id+"F2.opPattern","COPY",BODY,{"derivedFrom":makeQuery(id+"F1.opRevolve","SWEPT_BODY",BODY,{"disambiguationData":[OSD([sQuery(id+"F0.wireOp",EDGE,"E1")])]}),"instanceName":"1"}),"instanceName":"1"}),"instanceName":"1"}),"instanceName":"1"}),"instanceName":"1"}),"instanceName":"1"}),"instanceName":"1"});
            var Q359;
            Q359=makeQuery(id+"F10.opPattern","COPY",BODY,{"derivedFrom":makeQuery(id+"F9.opPattern","COPY",BODY,{"derivedFrom":makeQuery(id+"F8.opPattern","COPY",BODY,{"derivedFrom":makeQuery(id+"F6.opPattern","COPY",BODY,{"derivedFrom":makeQuery(id+"F5.opPattern","COPY",BODY,{"derivedFrom":makeQuery(id+"F4.opPattern","COPY",BODY,{"derivedFrom":makeQuery(id+"F3.opPattern","COPY",BODY,{"derivedFrom":makeQuery(id+"F2.opPattern","COPY",BODY,{"derivedFrom":makeQuery(id+"F1.opRevolve","SWEPT_BODY",BODY,{"disambiguationData":[OSD([sQuery(id+"F0.wireOp",EDGE,"E1")])]}),"instanceName":"1"}),"instanceName":"1"}),"instanceName":"1"}),"instanceName":"1"}),"instanceName":"1"}),"instanceName":"1"}),"instanceName":"1"}),"instanceName":"1"});
            var Q360;
            Q360=makeQuery(id+"F10.opPattern","COPY",BODY,{"derivedFrom":makeQuery(id+"F9.opPattern","COPY",BODY,{"derivedFrom":makeQuery(id+"F8.opPattern","COPY",BODY,{"derivedFrom":makeQuery(id+"F7.opPattern","COPY",BODY,{"derivedFrom":makeQuery(id+"F1.opRevolve","SWEPT_BODY",BODY,{"disambiguationData":[OSD([sQuery(id+"F0.wireOp",EDGE,"E1")])]}),"instanceName":"1"}),"instanceName":"1"}),"instanceName":"1"}),"instanceName":"1"});
            var Q361;
            Q361=makeQuery(id+"F10.opPattern","COPY",BODY,{"derivedFrom":makeQuery(id+"F9.opPattern","COPY",BODY,{"derivedFrom":makeQuery(id+"F8.opPattern","COPY",BODY,{"derivedFrom":makeQuery(id+"F7.opPattern","COPY",BODY,{"derivedFrom":makeQuery(id+"F2.opPattern","COPY",BODY,{"derivedFrom":makeQuery(id+"F1.opRevolve","SWEPT_BODY",BODY,{"disambiguationData":[OSD([sQuery(id+"F0.wireOp",EDGE,"E1")])]}),"instanceName":"1"}),"instanceName":"1"}),"instanceName":"1"}),"instanceName":"1"}),"instanceName":"1"});
            var Q362;
            Q362=makeQuery(id+"F10.opPattern","COPY",BODY,{"derivedFrom":makeQuery(id+"F9.opPattern","COPY",BODY,{"derivedFrom":makeQuery(id+"F8.opPattern","COPY",BODY,{"derivedFrom":makeQuery(id+"F7.opPattern","COPY",BODY,{"derivedFrom":makeQuery(id+"F3.opPattern","COPY",BODY,{"derivedFrom":makeQuery(id+"F2.opPattern","COPY",BODY,{"derivedFrom":makeQuery(id+"F1.opRevolve","SWEPT_BODY",BODY,{"disambiguationData":[OSD([sQuery(id+"F0.wireOp",EDGE,"E1")])]}),"instanceName":"1"}),"instanceName":"1"}),"instanceName":"1"}),"instanceName":"1"}),"instanceName":"1"}),"instanceName":"1"});
            var Q363;
            Q363=makeQuery(id+"F10.opPattern","COPY",BODY,{"derivedFrom":makeQuery(id+"F9.opPattern","COPY",BODY,{"derivedFrom":makeQuery(id+"F8.opPattern","COPY",BODY,{"derivedFrom":makeQuery(id+"F7.opPattern","COPY",BODY,{"derivedFrom":makeQuery(id+"F4.opPattern","COPY",BODY,{"derivedFrom":makeQuery(id+"F1.opRevolve","SWEPT_BODY",BODY,{"disambiguationData":[OSD([sQuery(id+"F0.wireOp",EDGE,"E1")])]}),"instanceName":"1"}),"instanceName":"1"}),"instanceName":"1"}),"instanceName":"1"}),"instanceName":"1"});
            var Q364;
            Q364=makeQuery(id+"F10.opPattern","COPY",BODY,{"derivedFrom":makeQuery(id+"F9.opPattern","COPY",BODY,{"derivedFrom":makeQuery(id+"F8.opPattern","COPY",BODY,{"derivedFrom":makeQuery(id+"F7.opPattern","COPY",BODY,{"derivedFrom":makeQuery(id+"F4.opPattern","COPY",BODY,{"derivedFrom":makeQuery(id+"F2.opPattern","COPY",BODY,{"derivedFrom":makeQuery(id+"F1.opRevolve","SWEPT_BODY",BODY,{"disambiguationData":[OSD([sQuery(id+"F0.wireOp",EDGE,"E1")])]}),"instanceName":"1"}),"instanceName":"1"}),"instanceName":"1"}),"instanceName":"1"}),"instanceName":"1"}),"instanceName":"1"});
            var Q365;
            Q365=makeQuery(id+"F10.opPattern","COPY",BODY,{"derivedFrom":makeQuery(id+"F9.opPattern","COPY",BODY,{"derivedFrom":makeQuery(id+"F8.opPattern","COPY",BODY,{"derivedFrom":makeQuery(id+"F7.opPattern","COPY",BODY,{"derivedFrom":makeQuery(id+"F4.opPattern","COPY",BODY,{"derivedFrom":makeQuery(id+"F3.opPattern","COPY",BODY,{"derivedFrom":makeQuery(id+"F2.opPattern","COPY",BODY,{"derivedFrom":makeQuery(id+"F1.opRevolve","SWEPT_BODY",BODY,{"disambiguationData":[OSD([sQuery(id+"F0.wireOp",EDGE,"E1")])]}),"instanceName":"1"}),"instanceName":"1"}),"instanceName":"1"}),"instanceName":"1"}),"instanceName":"1"}),"instanceName":"1"}),"instanceName":"1"});
            var Q366;
            Q366=makeQuery(id+"F10.opPattern","COPY",BODY,{"derivedFrom":makeQuery(id+"F9.opPattern","COPY",BODY,{"derivedFrom":makeQuery(id+"F8.opPattern","COPY",BODY,{"derivedFrom":makeQuery(id+"F7.opPattern","COPY",BODY,{"derivedFrom":makeQuery(id+"F5.opPattern","COPY",BODY,{"derivedFrom":makeQuery(id+"F1.opRevolve","SWEPT_BODY",BODY,{"disambiguationData":[OSD([sQuery(id+"F0.wireOp",EDGE,"E1")])]}),"instanceName":"1"}),"instanceName":"1"}),"instanceName":"1"}),"instanceName":"1"}),"instanceName":"1"});
            var Q367;
            Q367=makeQuery(id+"F10.opPattern","COPY",BODY,{"derivedFrom":makeQuery(id+"F9.opPattern","COPY",BODY,{"derivedFrom":makeQuery(id+"F8.opPattern","COPY",BODY,{"derivedFrom":makeQuery(id+"F7.opPattern","COPY",BODY,{"derivedFrom":makeQuery(id+"F5.opPattern","COPY",BODY,{"derivedFrom":makeQuery(id+"F2.opPattern","COPY",BODY,{"derivedFrom":makeQuery(id+"F1.opRevolve","SWEPT_BODY",BODY,{"disambiguationData":[OSD([sQuery(id+"F0.wireOp",EDGE,"E1")])]}),"instanceName":"1"}),"instanceName":"1"}),"instanceName":"1"}),"instanceName":"1"}),"instanceName":"1"}),"instanceName":"1"});
            var Q368;
            Q368=makeQuery(id+"F10.opPattern","COPY",BODY,{"derivedFrom":makeQuery(id+"F9.opPattern","COPY",BODY,{"derivedFrom":makeQuery(id+"F8.opPattern","COPY",BODY,{"derivedFrom":makeQuery(id+"F7.opPattern","COPY",BODY,{"derivedFrom":makeQuery(id+"F5.opPattern","COPY",BODY,{"derivedFrom":makeQuery(id+"F3.opPattern","COPY",BODY,{"derivedFrom":makeQuery(id+"F2.opPattern","COPY",BODY,{"derivedFrom":makeQuery(id+"F1.opRevolve","SWEPT_BODY",BODY,{"disambiguationData":[OSD([sQuery(id+"F0.wireOp",EDGE,"E1")])]}),"instanceName":"1"}),"instanceName":"1"}),"instanceName":"1"}),"instanceName":"1"}),"instanceName":"1"}),"instanceName":"1"}),"instanceName":"1"});
            var Q369;
            Q369=makeQuery(id+"F10.opPattern","COPY",BODY,{"derivedFrom":makeQuery(id+"F9.opPattern","COPY",BODY,{"derivedFrom":makeQuery(id+"F8.opPattern","COPY",BODY,{"derivedFrom":makeQuery(id+"F7.opPattern","COPY",BODY,{"derivedFrom":makeQuery(id+"F5.opPattern","COPY",BODY,{"derivedFrom":makeQuery(id+"F4.opPattern","COPY",BODY,{"derivedFrom":makeQuery(id+"F1.opRevolve","SWEPT_BODY",BODY,{"disambiguationData":[OSD([sQuery(id+"F0.wireOp",EDGE,"E1")])]}),"instanceName":"1"}),"instanceName":"1"}),"instanceName":"1"}),"instanceName":"1"}),"instanceName":"1"}),"instanceName":"1"});
            var Q370;
            Q370=makeQuery(id+"F10.opPattern","COPY",BODY,{"derivedFrom":makeQuery(id+"F9.opPattern","COPY",BODY,{"derivedFrom":makeQuery(id+"F8.opPattern","COPY",BODY,{"derivedFrom":makeQuery(id+"F7.opPattern","COPY",BODY,{"derivedFrom":makeQuery(id+"F5.opPattern","COPY",BODY,{"derivedFrom":makeQuery(id+"F4.opPattern","COPY",BODY,{"derivedFrom":makeQuery(id+"F2.opPattern","COPY",BODY,{"derivedFrom":makeQuery(id+"F1.opRevolve","SWEPT_BODY",BODY,{"disambiguationData":[OSD([sQuery(id+"F0.wireOp",EDGE,"E1")])]}),"instanceName":"1"}),"instanceName":"1"}),"instanceName":"1"}),"instanceName":"1"}),"instanceName":"1"}),"instanceName":"1"}),"instanceName":"1"});
            var Q371;
            Q371=makeQuery(id+"F10.opPattern","COPY",BODY,{"derivedFrom":makeQuery(id+"F9.opPattern","COPY",BODY,{"derivedFrom":makeQuery(id+"F8.opPattern","COPY",BODY,{"derivedFrom":makeQuery(id+"F7.opPattern","COPY",BODY,{"derivedFrom":makeQuery(id+"F5.opPattern","COPY",BODY,{"derivedFrom":makeQuery(id+"F4.opPattern","COPY",BODY,{"derivedFrom":makeQuery(id+"F3.opPattern","COPY",BODY,{"derivedFrom":makeQuery(id+"F2.opPattern","COPY",BODY,{"derivedFrom":makeQuery(id+"F1.opRevolve","SWEPT_BODY",BODY,{"disambiguationData":[OSD([sQuery(id+"F0.wireOp",EDGE,"E1")])]}),"instanceName":"1"}),"instanceName":"1"}),"instanceName":"1"}),"instanceName":"1"}),"instanceName":"1"}),"instanceName":"1"}),"instanceName":"1"}),"instanceName":"1"});
            var Q372;
            Q372=makeQuery(id+"F10.opPattern","COPY",BODY,{"derivedFrom":makeQuery(id+"F9.opPattern","COPY",BODY,{"derivedFrom":makeQuery(id+"F8.opPattern","COPY",BODY,{"derivedFrom":makeQuery(id+"F7.opPattern","COPY",BODY,{"derivedFrom":makeQuery(id+"F6.opPattern","COPY",BODY,{"derivedFrom":makeQuery(id+"F1.opRevolve","SWEPT_BODY",BODY,{"disambiguationData":[OSD([sQuery(id+"F0.wireOp",EDGE,"E1")])]}),"instanceName":"1"}),"instanceName":"1"}),"instanceName":"1"}),"instanceName":"1"}),"instanceName":"1"});
            var Q373;
            Q373=makeQuery(id+"F10.opPattern","COPY",BODY,{"derivedFrom":makeQuery(id+"F9.opPattern","COPY",BODY,{"derivedFrom":makeQuery(id+"F8.opPattern","COPY",BODY,{"derivedFrom":makeQuery(id+"F7.opPattern","COPY",BODY,{"derivedFrom":makeQuery(id+"F6.opPattern","COPY",BODY,{"derivedFrom":makeQuery(id+"F2.opPattern","COPY",BODY,{"derivedFrom":makeQuery(id+"F1.opRevolve","SWEPT_BODY",BODY,{"disambiguationData":[OSD([sQuery(id+"F0.wireOp",EDGE,"E1")])]}),"instanceName":"1"}),"instanceName":"1"}),"instanceName":"1"}),"instanceName":"1"}),"instanceName":"1"}),"instanceName":"1"});
            var Q374;
            Q374=makeQuery(id+"F10.opPattern","COPY",BODY,{"derivedFrom":makeQuery(id+"F9.opPattern","COPY",BODY,{"derivedFrom":makeQuery(id+"F8.opPattern","COPY",BODY,{"derivedFrom":makeQuery(id+"F7.opPattern","COPY",BODY,{"derivedFrom":makeQuery(id+"F6.opPattern","COPY",BODY,{"derivedFrom":makeQuery(id+"F3.opPattern","COPY",BODY,{"derivedFrom":makeQuery(id+"F2.opPattern","COPY",BODY,{"derivedFrom":makeQuery(id+"F1.opRevolve","SWEPT_BODY",BODY,{"disambiguationData":[OSD([sQuery(id+"F0.wireOp",EDGE,"E1")])]}),"instanceName":"1"}),"instanceName":"1"}),"instanceName":"1"}),"instanceName":"1"}),"instanceName":"1"}),"instanceName":"1"}),"instanceName":"1"});
            var Q375;
            Q375=makeQuery(id+"F10.opPattern","COPY",BODY,{"derivedFrom":makeQuery(id+"F9.opPattern","COPY",BODY,{"derivedFrom":makeQuery(id+"F8.opPattern","COPY",BODY,{"derivedFrom":makeQuery(id+"F7.opPattern","COPY",BODY,{"derivedFrom":makeQuery(id+"F6.opPattern","COPY",BODY,{"derivedFrom":makeQuery(id+"F4.opPattern","COPY",BODY,{"derivedFrom":makeQuery(id+"F1.opRevolve","SWEPT_BODY",BODY,{"disambiguationData":[OSD([sQuery(id+"F0.wireOp",EDGE,"E1")])]}),"instanceName":"1"}),"instanceName":"1"}),"instanceName":"1"}),"instanceName":"1"}),"instanceName":"1"}),"instanceName":"1"});
            var Q376;
            Q376=makeQuery(id+"F10.opPattern","COPY",BODY,{"derivedFrom":makeQuery(id+"F9.opPattern","COPY",BODY,{"derivedFrom":makeQuery(id+"F8.opPattern","COPY",BODY,{"derivedFrom":makeQuery(id+"F7.opPattern","COPY",BODY,{"derivedFrom":makeQuery(id+"F6.opPattern","COPY",BODY,{"derivedFrom":makeQuery(id+"F4.opPattern","COPY",BODY,{"derivedFrom":makeQuery(id+"F2.opPattern","COPY",BODY,{"derivedFrom":makeQuery(id+"F1.opRevolve","SWEPT_BODY",BODY,{"disambiguationData":[OSD([sQuery(id+"F0.wireOp",EDGE,"E1")])]}),"instanceName":"1"}),"instanceName":"1"}),"instanceName":"1"}),"instanceName":"1"}),"instanceName":"1"}),"instanceName":"1"}),"instanceName":"1"});
            var Q377;
            Q377=makeQuery(id+"F10.opPattern","COPY",BODY,{"derivedFrom":makeQuery(id+"F9.opPattern","COPY",BODY,{"derivedFrom":makeQuery(id+"F8.opPattern","COPY",BODY,{"derivedFrom":makeQuery(id+"F7.opPattern","COPY",BODY,{"derivedFrom":makeQuery(id+"F6.opPattern","COPY",BODY,{"derivedFrom":makeQuery(id+"F4.opPattern","COPY",BODY,{"derivedFrom":makeQuery(id+"F3.opPattern","COPY",BODY,{"derivedFrom":makeQuery(id+"F2.opPattern","COPY",BODY,{"derivedFrom":makeQuery(id+"F1.opRevolve","SWEPT_BODY",BODY,{"disambiguationData":[OSD([sQuery(id+"F0.wireOp",EDGE,"E1")])]}),"instanceName":"1"}),"instanceName":"1"}),"instanceName":"1"}),"instanceName":"1"}),"instanceName":"1"}),"instanceName":"1"}),"instanceName":"1"}),"instanceName":"1"});
            var Q378;
            Q378=makeQuery(id+"F10.opPattern","COPY",BODY,{"derivedFrom":makeQuery(id+"F9.opPattern","COPY",BODY,{"derivedFrom":makeQuery(id+"F8.opPattern","COPY",BODY,{"derivedFrom":makeQuery(id+"F7.opPattern","COPY",BODY,{"derivedFrom":makeQuery(id+"F6.opPattern","COPY",BODY,{"derivedFrom":makeQuery(id+"F5.opPattern","COPY",BODY,{"derivedFrom":makeQuery(id+"F1.opRevolve","SWEPT_BODY",BODY,{"disambiguationData":[OSD([sQuery(id+"F0.wireOp",EDGE,"E1")])]}),"instanceName":"1"}),"instanceName":"1"}),"instanceName":"1"}),"instanceName":"1"}),"instanceName":"1"}),"instanceName":"1"});
            var Q379;
            Q379=makeQuery(id+"F10.opPattern","COPY",BODY,{"derivedFrom":makeQuery(id+"F9.opPattern","COPY",BODY,{"derivedFrom":makeQuery(id+"F8.opPattern","COPY",BODY,{"derivedFrom":makeQuery(id+"F7.opPattern","COPY",BODY,{"derivedFrom":makeQuery(id+"F6.opPattern","COPY",BODY,{"derivedFrom":makeQuery(id+"F5.opPattern","COPY",BODY,{"derivedFrom":makeQuery(id+"F2.opPattern","COPY",BODY,{"derivedFrom":makeQuery(id+"F1.opRevolve","SWEPT_BODY",BODY,{"disambiguationData":[OSD([sQuery(id+"F0.wireOp",EDGE,"E1")])]}),"instanceName":"1"}),"instanceName":"1"}),"instanceName":"1"}),"instanceName":"1"}),"instanceName":"1"}),"instanceName":"1"}),"instanceName":"1"});
            var Q380;
            Q380=makeQuery(id+"F10.opPattern","COPY",BODY,{"derivedFrom":makeQuery(id+"F9.opPattern","COPY",BODY,{"derivedFrom":makeQuery(id+"F8.opPattern","COPY",BODY,{"derivedFrom":makeQuery(id+"F7.opPattern","COPY",BODY,{"derivedFrom":makeQuery(id+"F6.opPattern","COPY",BODY,{"derivedFrom":makeQuery(id+"F5.opPattern","COPY",BODY,{"derivedFrom":makeQuery(id+"F3.opPattern","COPY",BODY,{"derivedFrom":makeQuery(id+"F2.opPattern","COPY",BODY,{"derivedFrom":makeQuery(id+"F1.opRevolve","SWEPT_BODY",BODY,{"disambiguationData":[OSD([sQuery(id+"F0.wireOp",EDGE,"E1")])]}),"instanceName":"1"}),"instanceName":"1"}),"instanceName":"1"}),"instanceName":"1"}),"instanceName":"1"}),"instanceName":"1"}),"instanceName":"1"}),"instanceName":"1"});
            var Q381;
            Q381=makeQuery(id+"F10.opPattern","COPY",BODY,{"derivedFrom":makeQuery(id+"F9.opPattern","COPY",BODY,{"derivedFrom":makeQuery(id+"F8.opPattern","COPY",BODY,{"derivedFrom":makeQuery(id+"F7.opPattern","COPY",BODY,{"derivedFrom":makeQuery(id+"F6.opPattern","COPY",BODY,{"derivedFrom":makeQuery(id+"F5.opPattern","COPY",BODY,{"derivedFrom":makeQuery(id+"F4.opPattern","COPY",BODY,{"derivedFrom":makeQuery(id+"F1.opRevolve","SWEPT_BODY",BODY,{"disambiguationData":[OSD([sQuery(id+"F0.wireOp",EDGE,"E1")])]}),"instanceName":"1"}),"instanceName":"1"}),"instanceName":"1"}),"instanceName":"1"}),"instanceName":"1"}),"instanceName":"1"}),"instanceName":"1"});
            var Q382;
            Q382=makeQuery(id+"F10.opPattern","COPY",BODY,{"derivedFrom":makeQuery(id+"F9.opPattern","COPY",BODY,{"derivedFrom":makeQuery(id+"F8.opPattern","COPY",BODY,{"derivedFrom":makeQuery(id+"F7.opPattern","COPY",BODY,{"derivedFrom":makeQuery(id+"F6.opPattern","COPY",BODY,{"derivedFrom":makeQuery(id+"F5.opPattern","COPY",BODY,{"derivedFrom":makeQuery(id+"F4.opPattern","COPY",BODY,{"derivedFrom":makeQuery(id+"F2.opPattern","COPY",BODY,{"derivedFrom":makeQuery(id+"F1.opRevolve","SWEPT_BODY",BODY,{"disambiguationData":[OSD([sQuery(id+"F0.wireOp",EDGE,"E1")])]}),"instanceName":"1"}),"instanceName":"1"}),"instanceName":"1"}),"instanceName":"1"}),"instanceName":"1"}),"instanceName":"1"}),"instanceName":"1"}),"instanceName":"1"});
            var Q383;
            Q383=makeQuery(id+"F10.opPattern","COPY",BODY,{"derivedFrom":makeQuery(id+"F9.opPattern","COPY",BODY,{"derivedFrom":makeQuery(id+"F8.opPattern","COPY",BODY,{"derivedFrom":makeQuery(id+"F7.opPattern","COPY",BODY,{"derivedFrom":makeQuery(id+"F6.opPattern","COPY",BODY,{"derivedFrom":makeQuery(id+"F5.opPattern","COPY",BODY,{"derivedFrom":makeQuery(id+"F4.opPattern","COPY",BODY,{"derivedFrom":makeQuery(id+"F3.opPattern","COPY",BODY,{"derivedFrom":makeQuery(id+"F2.opPattern","COPY",BODY,{"derivedFrom":makeQuery(id+"F1.opRevolve","SWEPT_BODY",BODY,{"disambiguationData":[OSD([sQuery(id+"F0.wireOp",EDGE,"E1")])]}),"instanceName":"1"}),"instanceName":"1"}),"instanceName":"1"}),"instanceName":"1"}),"instanceName":"1"}),"instanceName":"1"}),"instanceName":"1"}),"instanceName":"1"}),"instanceName":"1"});
            var Q384;
            Q384=makeQuery(id+"F11.opPattern","COPY",BODY,{"derivedFrom":makeQuery(id+"F1.opRevolve","SWEPT_BODY",BODY,{"disambiguationData":[OSD([sQuery(id+"F0.wireOp",EDGE,"E1")])]}),"instanceName":"1"});
            var Q385;
            Q385=makeQuery(id+"F11.opPattern","COPY",BODY,{"derivedFrom":makeQuery(id+"F2.opPattern","COPY",BODY,{"derivedFrom":makeQuery(id+"F1.opRevolve","SWEPT_BODY",BODY,{"disambiguationData":[OSD([sQuery(id+"F0.wireOp",EDGE,"E1")])]}),"instanceName":"1"}),"instanceName":"1"});
            var Q386;
            Q386=makeQuery(id+"F11.opPattern","COPY",BODY,{"derivedFrom":makeQuery(id+"F3.opPattern","COPY",BODY,{"derivedFrom":makeQuery(id+"F2.opPattern","COPY",BODY,{"derivedFrom":makeQuery(id+"F1.opRevolve","SWEPT_BODY",BODY,{"disambiguationData":[OSD([sQuery(id+"F0.wireOp",EDGE,"E1")])]}),"instanceName":"1"}),"instanceName":"1"}),"instanceName":"1"});
            var Q387;
            Q387=makeQuery(id+"F11.opPattern","COPY",BODY,{"derivedFrom":makeQuery(id+"F4.opPattern","COPY",BODY,{"derivedFrom":makeQuery(id+"F1.opRevolve","SWEPT_BODY",BODY,{"disambiguationData":[OSD([sQuery(id+"F0.wireOp",EDGE,"E1")])]}),"instanceName":"1"}),"instanceName":"1"});
            var Q388;
            Q388=makeQuery(id+"F11.opPattern","COPY",BODY,{"derivedFrom":makeQuery(id+"F4.opPattern","COPY",BODY,{"derivedFrom":makeQuery(id+"F2.opPattern","COPY",BODY,{"derivedFrom":makeQuery(id+"F1.opRevolve","SWEPT_BODY",BODY,{"disambiguationData":[OSD([sQuery(id+"F0.wireOp",EDGE,"E1")])]}),"instanceName":"1"}),"instanceName":"1"}),"instanceName":"1"});
            var Q389;
            Q389=makeQuery(id+"F11.opPattern","COPY",BODY,{"derivedFrom":makeQuery(id+"F4.opPattern","COPY",BODY,{"derivedFrom":makeQuery(id+"F3.opPattern","COPY",BODY,{"derivedFrom":makeQuery(id+"F2.opPattern","COPY",BODY,{"derivedFrom":makeQuery(id+"F1.opRevolve","SWEPT_BODY",BODY,{"disambiguationData":[OSD([sQuery(id+"F0.wireOp",EDGE,"E1")])]}),"instanceName":"1"}),"instanceName":"1"}),"instanceName":"1"}),"instanceName":"1"});
            var Q390;
            Q390=makeQuery(id+"F11.opPattern","COPY",BODY,{"derivedFrom":makeQuery(id+"F5.opPattern","COPY",BODY,{"derivedFrom":makeQuery(id+"F1.opRevolve","SWEPT_BODY",BODY,{"disambiguationData":[OSD([sQuery(id+"F0.wireOp",EDGE,"E1")])]}),"instanceName":"1"}),"instanceName":"1"});
            var Q391;
            Q391=makeQuery(id+"F11.opPattern","COPY",BODY,{"derivedFrom":makeQuery(id+"F5.opPattern","COPY",BODY,{"derivedFrom":makeQuery(id+"F2.opPattern","COPY",BODY,{"derivedFrom":makeQuery(id+"F1.opRevolve","SWEPT_BODY",BODY,{"disambiguationData":[OSD([sQuery(id+"F0.wireOp",EDGE,"E1")])]}),"instanceName":"1"}),"instanceName":"1"}),"instanceName":"1"});
            var Q392;
            Q392=makeQuery(id+"F11.opPattern","COPY",BODY,{"derivedFrom":makeQuery(id+"F5.opPattern","COPY",BODY,{"derivedFrom":makeQuery(id+"F3.opPattern","COPY",BODY,{"derivedFrom":makeQuery(id+"F2.opPattern","COPY",BODY,{"derivedFrom":makeQuery(id+"F1.opRevolve","SWEPT_BODY",BODY,{"disambiguationData":[OSD([sQuery(id+"F0.wireOp",EDGE,"E1")])]}),"instanceName":"1"}),"instanceName":"1"}),"instanceName":"1"}),"instanceName":"1"});
            var Q393;
            Q393=makeQuery(id+"F11.opPattern","COPY",BODY,{"derivedFrom":makeQuery(id+"F5.opPattern","COPY",BODY,{"derivedFrom":makeQuery(id+"F4.opPattern","COPY",BODY,{"derivedFrom":makeQuery(id+"F1.opRevolve","SWEPT_BODY",BODY,{"disambiguationData":[OSD([sQuery(id+"F0.wireOp",EDGE,"E1")])]}),"instanceName":"1"}),"instanceName":"1"}),"instanceName":"1"});
            var Q394;
            Q394=makeQuery(id+"F11.opPattern","COPY",BODY,{"derivedFrom":makeQuery(id+"F5.opPattern","COPY",BODY,{"derivedFrom":makeQuery(id+"F4.opPattern","COPY",BODY,{"derivedFrom":makeQuery(id+"F2.opPattern","COPY",BODY,{"derivedFrom":makeQuery(id+"F1.opRevolve","SWEPT_BODY",BODY,{"disambiguationData":[OSD([sQuery(id+"F0.wireOp",EDGE,"E1")])]}),"instanceName":"1"}),"instanceName":"1"}),"instanceName":"1"}),"instanceName":"1"});
            var Q395;
            Q395=makeQuery(id+"F11.opPattern","COPY",BODY,{"derivedFrom":makeQuery(id+"F5.opPattern","COPY",BODY,{"derivedFrom":makeQuery(id+"F4.opPattern","COPY",BODY,{"derivedFrom":makeQuery(id+"F3.opPattern","COPY",BODY,{"derivedFrom":makeQuery(id+"F2.opPattern","COPY",BODY,{"derivedFrom":makeQuery(id+"F1.opRevolve","SWEPT_BODY",BODY,{"disambiguationData":[OSD([sQuery(id+"F0.wireOp",EDGE,"E1")])]}),"instanceName":"1"}),"instanceName":"1"}),"instanceName":"1"}),"instanceName":"1"}),"instanceName":"1"});
            var Q396;
            Q396=makeQuery(id+"F11.opPattern","COPY",BODY,{"derivedFrom":makeQuery(id+"F6.opPattern","COPY",BODY,{"derivedFrom":makeQuery(id+"F1.opRevolve","SWEPT_BODY",BODY,{"disambiguationData":[OSD([sQuery(id+"F0.wireOp",EDGE,"E1")])]}),"instanceName":"1"}),"instanceName":"1"});
            var Q397;
            Q397=makeQuery(id+"F11.opPattern","COPY",BODY,{"derivedFrom":makeQuery(id+"F6.opPattern","COPY",BODY,{"derivedFrom":makeQuery(id+"F2.opPattern","COPY",BODY,{"derivedFrom":makeQuery(id+"F1.opRevolve","SWEPT_BODY",BODY,{"disambiguationData":[OSD([sQuery(id+"F0.wireOp",EDGE,"E1")])]}),"instanceName":"1"}),"instanceName":"1"}),"instanceName":"1"});
            var Q398;
            Q398=makeQuery(id+"F11.opPattern","COPY",BODY,{"derivedFrom":makeQuery(id+"F6.opPattern","COPY",BODY,{"derivedFrom":makeQuery(id+"F3.opPattern","COPY",BODY,{"derivedFrom":makeQuery(id+"F2.opPattern","COPY",BODY,{"derivedFrom":makeQuery(id+"F1.opRevolve","SWEPT_BODY",BODY,{"disambiguationData":[OSD([sQuery(id+"F0.wireOp",EDGE,"E1")])]}),"instanceName":"1"}),"instanceName":"1"}),"instanceName":"1"}),"instanceName":"1"});
            var Q399;
            Q399=makeQuery(id+"F11.opPattern","COPY",BODY,{"derivedFrom":makeQuery(id+"F6.opPattern","COPY",BODY,{"derivedFrom":makeQuery(id+"F4.opPattern","COPY",BODY,{"derivedFrom":makeQuery(id+"F1.opRevolve","SWEPT_BODY",BODY,{"disambiguationData":[OSD([sQuery(id+"F0.wireOp",EDGE,"E1")])]}),"instanceName":"1"}),"instanceName":"1"}),"instanceName":"1"});
            var Q400;
            Q400=makeQuery(id+"F11.opPattern","COPY",BODY,{"derivedFrom":makeQuery(id+"F6.opPattern","COPY",BODY,{"derivedFrom":makeQuery(id+"F4.opPattern","COPY",BODY,{"derivedFrom":makeQuery(id+"F2.opPattern","COPY",BODY,{"derivedFrom":makeQuery(id+"F1.opRevolve","SWEPT_BODY",BODY,{"disambiguationData":[OSD([sQuery(id+"F0.wireOp",EDGE,"E1")])]}),"instanceName":"1"}),"instanceName":"1"}),"instanceName":"1"}),"instanceName":"1"});
            var Q401;
            Q401=makeQuery(id+"F11.opPattern","COPY",BODY,{"derivedFrom":makeQuery(id+"F6.opPattern","COPY",BODY,{"derivedFrom":makeQuery(id+"F4.opPattern","COPY",BODY,{"derivedFrom":makeQuery(id+"F3.opPattern","COPY",BODY,{"derivedFrom":makeQuery(id+"F2.opPattern","COPY",BODY,{"derivedFrom":makeQuery(id+"F1.opRevolve","SWEPT_BODY",BODY,{"disambiguationData":[OSD([sQuery(id+"F0.wireOp",EDGE,"E1")])]}),"instanceName":"1"}),"instanceName":"1"}),"instanceName":"1"}),"instanceName":"1"}),"instanceName":"1"});
            var Q402;
            Q402=makeQuery(id+"F11.opPattern","COPY",BODY,{"derivedFrom":makeQuery(id+"F6.opPattern","COPY",BODY,{"derivedFrom":makeQuery(id+"F5.opPattern","COPY",BODY,{"derivedFrom":makeQuery(id+"F1.opRevolve","SWEPT_BODY",BODY,{"disambiguationData":[OSD([sQuery(id+"F0.wireOp",EDGE,"E1")])]}),"instanceName":"1"}),"instanceName":"1"}),"instanceName":"1"});
            var Q403;
            Q403=makeQuery(id+"F11.opPattern","COPY",BODY,{"derivedFrom":makeQuery(id+"F6.opPattern","COPY",BODY,{"derivedFrom":makeQuery(id+"F5.opPattern","COPY",BODY,{"derivedFrom":makeQuery(id+"F2.opPattern","COPY",BODY,{"derivedFrom":makeQuery(id+"F1.opRevolve","SWEPT_BODY",BODY,{"disambiguationData":[OSD([sQuery(id+"F0.wireOp",EDGE,"E1")])]}),"instanceName":"1"}),"instanceName":"1"}),"instanceName":"1"}),"instanceName":"1"});
            var Q404;
            Q404=makeQuery(id+"F11.opPattern","COPY",BODY,{"derivedFrom":makeQuery(id+"F6.opPattern","COPY",BODY,{"derivedFrom":makeQuery(id+"F5.opPattern","COPY",BODY,{"derivedFrom":makeQuery(id+"F3.opPattern","COPY",BODY,{"derivedFrom":makeQuery(id+"F2.opPattern","COPY",BODY,{"derivedFrom":makeQuery(id+"F1.opRevolve","SWEPT_BODY",BODY,{"disambiguationData":[OSD([sQuery(id+"F0.wireOp",EDGE,"E1")])]}),"instanceName":"1"}),"instanceName":"1"}),"instanceName":"1"}),"instanceName":"1"}),"instanceName":"1"});
            var Q405;
            Q405=makeQuery(id+"F11.opPattern","COPY",BODY,{"derivedFrom":makeQuery(id+"F6.opPattern","COPY",BODY,{"derivedFrom":makeQuery(id+"F5.opPattern","COPY",BODY,{"derivedFrom":makeQuery(id+"F4.opPattern","COPY",BODY,{"derivedFrom":makeQuery(id+"F1.opRevolve","SWEPT_BODY",BODY,{"disambiguationData":[OSD([sQuery(id+"F0.wireOp",EDGE,"E1")])]}),"instanceName":"1"}),"instanceName":"1"}),"instanceName":"1"}),"instanceName":"1"});
            var Q406;
            Q406=makeQuery(id+"F11.opPattern","COPY",BODY,{"derivedFrom":makeQuery(id+"F6.opPattern","COPY",BODY,{"derivedFrom":makeQuery(id+"F5.opPattern","COPY",BODY,{"derivedFrom":makeQuery(id+"F4.opPattern","COPY",BODY,{"derivedFrom":makeQuery(id+"F2.opPattern","COPY",BODY,{"derivedFrom":makeQuery(id+"F1.opRevolve","SWEPT_BODY",BODY,{"disambiguationData":[OSD([sQuery(id+"F0.wireOp",EDGE,"E1")])]}),"instanceName":"1"}),"instanceName":"1"}),"instanceName":"1"}),"instanceName":"1"}),"instanceName":"1"});
            var Q407;
            Q407=makeQuery(id+"F11.opPattern","COPY",BODY,{"derivedFrom":makeQuery(id+"F6.opPattern","COPY",BODY,{"derivedFrom":makeQuery(id+"F5.opPattern","COPY",BODY,{"derivedFrom":makeQuery(id+"F4.opPattern","COPY",BODY,{"derivedFrom":makeQuery(id+"F3.opPattern","COPY",BODY,{"derivedFrom":makeQuery(id+"F2.opPattern","COPY",BODY,{"derivedFrom":makeQuery(id+"F1.opRevolve","SWEPT_BODY",BODY,{"disambiguationData":[OSD([sQuery(id+"F0.wireOp",EDGE,"E1")])]}),"instanceName":"1"}),"instanceName":"1"}),"instanceName":"1"}),"instanceName":"1"}),"instanceName":"1"}),"instanceName":"1"});
            var Q408;
            Q408=makeQuery(id+"F11.opPattern","COPY",BODY,{"derivedFrom":makeQuery(id+"F7.opPattern","COPY",BODY,{"derivedFrom":makeQuery(id+"F1.opRevolve","SWEPT_BODY",BODY,{"disambiguationData":[OSD([sQuery(id+"F0.wireOp",EDGE,"E1")])]}),"instanceName":"1"}),"instanceName":"1"});
            var Q409;
            Q409=makeQuery(id+"F11.opPattern","COPY",BODY,{"derivedFrom":makeQuery(id+"F7.opPattern","COPY",BODY,{"derivedFrom":makeQuery(id+"F2.opPattern","COPY",BODY,{"derivedFrom":makeQuery(id+"F1.opRevolve","SWEPT_BODY",BODY,{"disambiguationData":[OSD([sQuery(id+"F0.wireOp",EDGE,"E1")])]}),"instanceName":"1"}),"instanceName":"1"}),"instanceName":"1"});
            var Q410;
            Q410=makeQuery(id+"F11.opPattern","COPY",BODY,{"derivedFrom":makeQuery(id+"F7.opPattern","COPY",BODY,{"derivedFrom":makeQuery(id+"F3.opPattern","COPY",BODY,{"derivedFrom":makeQuery(id+"F2.opPattern","COPY",BODY,{"derivedFrom":makeQuery(id+"F1.opRevolve","SWEPT_BODY",BODY,{"disambiguationData":[OSD([sQuery(id+"F0.wireOp",EDGE,"E1")])]}),"instanceName":"1"}),"instanceName":"1"}),"instanceName":"1"}),"instanceName":"1"});
            var Q411;
            Q411=makeQuery(id+"F11.opPattern","COPY",BODY,{"derivedFrom":makeQuery(id+"F7.opPattern","COPY",BODY,{"derivedFrom":makeQuery(id+"F4.opPattern","COPY",BODY,{"derivedFrom":makeQuery(id+"F1.opRevolve","SWEPT_BODY",BODY,{"disambiguationData":[OSD([sQuery(id+"F0.wireOp",EDGE,"E1")])]}),"instanceName":"1"}),"instanceName":"1"}),"instanceName":"1"});
            var Q412;
            Q412=makeQuery(id+"F11.opPattern","COPY",BODY,{"derivedFrom":makeQuery(id+"F7.opPattern","COPY",BODY,{"derivedFrom":makeQuery(id+"F4.opPattern","COPY",BODY,{"derivedFrom":makeQuery(id+"F2.opPattern","COPY",BODY,{"derivedFrom":makeQuery(id+"F1.opRevolve","SWEPT_BODY",BODY,{"disambiguationData":[OSD([sQuery(id+"F0.wireOp",EDGE,"E1")])]}),"instanceName":"1"}),"instanceName":"1"}),"instanceName":"1"}),"instanceName":"1"});
            var Q413;
            Q413=makeQuery(id+"F11.opPattern","COPY",BODY,{"derivedFrom":makeQuery(id+"F7.opPattern","COPY",BODY,{"derivedFrom":makeQuery(id+"F4.opPattern","COPY",BODY,{"derivedFrom":makeQuery(id+"F3.opPattern","COPY",BODY,{"derivedFrom":makeQuery(id+"F2.opPattern","COPY",BODY,{"derivedFrom":makeQuery(id+"F1.opRevolve","SWEPT_BODY",BODY,{"disambiguationData":[OSD([sQuery(id+"F0.wireOp",EDGE,"E1")])]}),"instanceName":"1"}),"instanceName":"1"}),"instanceName":"1"}),"instanceName":"1"}),"instanceName":"1"});
            var Q414;
            Q414=makeQuery(id+"F11.opPattern","COPY",BODY,{"derivedFrom":makeQuery(id+"F7.opPattern","COPY",BODY,{"derivedFrom":makeQuery(id+"F5.opPattern","COPY",BODY,{"derivedFrom":makeQuery(id+"F1.opRevolve","SWEPT_BODY",BODY,{"disambiguationData":[OSD([sQuery(id+"F0.wireOp",EDGE,"E1")])]}),"instanceName":"1"}),"instanceName":"1"}),"instanceName":"1"});
            var Q415;
            Q415=makeQuery(id+"F11.opPattern","COPY",BODY,{"derivedFrom":makeQuery(id+"F7.opPattern","COPY",BODY,{"derivedFrom":makeQuery(id+"F5.opPattern","COPY",BODY,{"derivedFrom":makeQuery(id+"F2.opPattern","COPY",BODY,{"derivedFrom":makeQuery(id+"F1.opRevolve","SWEPT_BODY",BODY,{"disambiguationData":[OSD([sQuery(id+"F0.wireOp",EDGE,"E1")])]}),"instanceName":"1"}),"instanceName":"1"}),"instanceName":"1"}),"instanceName":"1"});
            var Q416;
            Q416=makeQuery(id+"F11.opPattern","COPY",BODY,{"derivedFrom":makeQuery(id+"F7.opPattern","COPY",BODY,{"derivedFrom":makeQuery(id+"F5.opPattern","COPY",BODY,{"derivedFrom":makeQuery(id+"F3.opPattern","COPY",BODY,{"derivedFrom":makeQuery(id+"F2.opPattern","COPY",BODY,{"derivedFrom":makeQuery(id+"F1.opRevolve","SWEPT_BODY",BODY,{"disambiguationData":[OSD([sQuery(id+"F0.wireOp",EDGE,"E1")])]}),"instanceName":"1"}),"instanceName":"1"}),"instanceName":"1"}),"instanceName":"1"}),"instanceName":"1"});
            var Q417;
            Q417=makeQuery(id+"F11.opPattern","COPY",BODY,{"derivedFrom":makeQuery(id+"F7.opPattern","COPY",BODY,{"derivedFrom":makeQuery(id+"F5.opPattern","COPY",BODY,{"derivedFrom":makeQuery(id+"F4.opPattern","COPY",BODY,{"derivedFrom":makeQuery(id+"F1.opRevolve","SWEPT_BODY",BODY,{"disambiguationData":[OSD([sQuery(id+"F0.wireOp",EDGE,"E1")])]}),"instanceName":"1"}),"instanceName":"1"}),"instanceName":"1"}),"instanceName":"1"});
            var Q418;
            Q418=makeQuery(id+"F11.opPattern","COPY",BODY,{"derivedFrom":makeQuery(id+"F7.opPattern","COPY",BODY,{"derivedFrom":makeQuery(id+"F5.opPattern","COPY",BODY,{"derivedFrom":makeQuery(id+"F4.opPattern","COPY",BODY,{"derivedFrom":makeQuery(id+"F2.opPattern","COPY",BODY,{"derivedFrom":makeQuery(id+"F1.opRevolve","SWEPT_BODY",BODY,{"disambiguationData":[OSD([sQuery(id+"F0.wireOp",EDGE,"E1")])]}),"instanceName":"1"}),"instanceName":"1"}),"instanceName":"1"}),"instanceName":"1"}),"instanceName":"1"});
            var Q419;
            Q419=makeQuery(id+"F11.opPattern","COPY",BODY,{"derivedFrom":makeQuery(id+"F7.opPattern","COPY",BODY,{"derivedFrom":makeQuery(id+"F5.opPattern","COPY",BODY,{"derivedFrom":makeQuery(id+"F4.opPattern","COPY",BODY,{"derivedFrom":makeQuery(id+"F3.opPattern","COPY",BODY,{"derivedFrom":makeQuery(id+"F2.opPattern","COPY",BODY,{"derivedFrom":makeQuery(id+"F1.opRevolve","SWEPT_BODY",BODY,{"disambiguationData":[OSD([sQuery(id+"F0.wireOp",EDGE,"E1")])]}),"instanceName":"1"}),"instanceName":"1"}),"instanceName":"1"}),"instanceName":"1"}),"instanceName":"1"}),"instanceName":"1"});
            var Q420;
            Q420=makeQuery(id+"F11.opPattern","COPY",BODY,{"derivedFrom":makeQuery(id+"F7.opPattern","COPY",BODY,{"derivedFrom":makeQuery(id+"F6.opPattern","COPY",BODY,{"derivedFrom":makeQuery(id+"F1.opRevolve","SWEPT_BODY",BODY,{"disambiguationData":[OSD([sQuery(id+"F0.wireOp",EDGE,"E1")])]}),"instanceName":"1"}),"instanceName":"1"}),"instanceName":"1"});
            var Q421;
            Q421=makeQuery(id+"F11.opPattern","COPY",BODY,{"derivedFrom":makeQuery(id+"F7.opPattern","COPY",BODY,{"derivedFrom":makeQuery(id+"F6.opPattern","COPY",BODY,{"derivedFrom":makeQuery(id+"F2.opPattern","COPY",BODY,{"derivedFrom":makeQuery(id+"F1.opRevolve","SWEPT_BODY",BODY,{"disambiguationData":[OSD([sQuery(id+"F0.wireOp",EDGE,"E1")])]}),"instanceName":"1"}),"instanceName":"1"}),"instanceName":"1"}),"instanceName":"1"});
            var Q422;
            Q422=makeQuery(id+"F11.opPattern","COPY",BODY,{"derivedFrom":makeQuery(id+"F7.opPattern","COPY",BODY,{"derivedFrom":makeQuery(id+"F6.opPattern","COPY",BODY,{"derivedFrom":makeQuery(id+"F3.opPattern","COPY",BODY,{"derivedFrom":makeQuery(id+"F2.opPattern","COPY",BODY,{"derivedFrom":makeQuery(id+"F1.opRevolve","SWEPT_BODY",BODY,{"disambiguationData":[OSD([sQuery(id+"F0.wireOp",EDGE,"E1")])]}),"instanceName":"1"}),"instanceName":"1"}),"instanceName":"1"}),"instanceName":"1"}),"instanceName":"1"});
            var Q423;
            Q423=makeQuery(id+"F11.opPattern","COPY",BODY,{"derivedFrom":makeQuery(id+"F7.opPattern","COPY",BODY,{"derivedFrom":makeQuery(id+"F6.opPattern","COPY",BODY,{"derivedFrom":makeQuery(id+"F4.opPattern","COPY",BODY,{"derivedFrom":makeQuery(id+"F1.opRevolve","SWEPT_BODY",BODY,{"disambiguationData":[OSD([sQuery(id+"F0.wireOp",EDGE,"E1")])]}),"instanceName":"1"}),"instanceName":"1"}),"instanceName":"1"}),"instanceName":"1"});
            var Q424;
            Q424=makeQuery(id+"F11.opPattern","COPY",BODY,{"derivedFrom":makeQuery(id+"F7.opPattern","COPY",BODY,{"derivedFrom":makeQuery(id+"F6.opPattern","COPY",BODY,{"derivedFrom":makeQuery(id+"F4.opPattern","COPY",BODY,{"derivedFrom":makeQuery(id+"F2.opPattern","COPY",BODY,{"derivedFrom":makeQuery(id+"F1.opRevolve","SWEPT_BODY",BODY,{"disambiguationData":[OSD([sQuery(id+"F0.wireOp",EDGE,"E1")])]}),"instanceName":"1"}),"instanceName":"1"}),"instanceName":"1"}),"instanceName":"1"}),"instanceName":"1"});
            var Q425;
            Q425=makeQuery(id+"F11.opPattern","COPY",BODY,{"derivedFrom":makeQuery(id+"F7.opPattern","COPY",BODY,{"derivedFrom":makeQuery(id+"F6.opPattern","COPY",BODY,{"derivedFrom":makeQuery(id+"F4.opPattern","COPY",BODY,{"derivedFrom":makeQuery(id+"F3.opPattern","COPY",BODY,{"derivedFrom":makeQuery(id+"F2.opPattern","COPY",BODY,{"derivedFrom":makeQuery(id+"F1.opRevolve","SWEPT_BODY",BODY,{"disambiguationData":[OSD([sQuery(id+"F0.wireOp",EDGE,"E1")])]}),"instanceName":"1"}),"instanceName":"1"}),"instanceName":"1"}),"instanceName":"1"}),"instanceName":"1"}),"instanceName":"1"});
            var Q426;
            Q426=makeQuery(id+"F11.opPattern","COPY",BODY,{"derivedFrom":makeQuery(id+"F7.opPattern","COPY",BODY,{"derivedFrom":makeQuery(id+"F6.opPattern","COPY",BODY,{"derivedFrom":makeQuery(id+"F5.opPattern","COPY",BODY,{"derivedFrom":makeQuery(id+"F1.opRevolve","SWEPT_BODY",BODY,{"disambiguationData":[OSD([sQuery(id+"F0.wireOp",EDGE,"E1")])]}),"instanceName":"1"}),"instanceName":"1"}),"instanceName":"1"}),"instanceName":"1"});
            var Q427;
            Q427=makeQuery(id+"F11.opPattern","COPY",BODY,{"derivedFrom":makeQuery(id+"F7.opPattern","COPY",BODY,{"derivedFrom":makeQuery(id+"F6.opPattern","COPY",BODY,{"derivedFrom":makeQuery(id+"F5.opPattern","COPY",BODY,{"derivedFrom":makeQuery(id+"F2.opPattern","COPY",BODY,{"derivedFrom":makeQuery(id+"F1.opRevolve","SWEPT_BODY",BODY,{"disambiguationData":[OSD([sQuery(id+"F0.wireOp",EDGE,"E1")])]}),"instanceName":"1"}),"instanceName":"1"}),"instanceName":"1"}),"instanceName":"1"}),"instanceName":"1"});
            var Q428;
            Q428=makeQuery(id+"F11.opPattern","COPY",BODY,{"derivedFrom":makeQuery(id+"F7.opPattern","COPY",BODY,{"derivedFrom":makeQuery(id+"F6.opPattern","COPY",BODY,{"derivedFrom":makeQuery(id+"F5.opPattern","COPY",BODY,{"derivedFrom":makeQuery(id+"F3.opPattern","COPY",BODY,{"derivedFrom":makeQuery(id+"F2.opPattern","COPY",BODY,{"derivedFrom":makeQuery(id+"F1.opRevolve","SWEPT_BODY",BODY,{"disambiguationData":[OSD([sQuery(id+"F0.wireOp",EDGE,"E1")])]}),"instanceName":"1"}),"instanceName":"1"}),"instanceName":"1"}),"instanceName":"1"}),"instanceName":"1"}),"instanceName":"1"});
            var Q429;
            Q429=makeQuery(id+"F11.opPattern","COPY",BODY,{"derivedFrom":makeQuery(id+"F7.opPattern","COPY",BODY,{"derivedFrom":makeQuery(id+"F6.opPattern","COPY",BODY,{"derivedFrom":makeQuery(id+"F5.opPattern","COPY",BODY,{"derivedFrom":makeQuery(id+"F4.opPattern","COPY",BODY,{"derivedFrom":makeQuery(id+"F1.opRevolve","SWEPT_BODY",BODY,{"disambiguationData":[OSD([sQuery(id+"F0.wireOp",EDGE,"E1")])]}),"instanceName":"1"}),"instanceName":"1"}),"instanceName":"1"}),"instanceName":"1"}),"instanceName":"1"});
            var Q430;
            Q430=makeQuery(id+"F11.opPattern","COPY",BODY,{"derivedFrom":makeQuery(id+"F7.opPattern","COPY",BODY,{"derivedFrom":makeQuery(id+"F6.opPattern","COPY",BODY,{"derivedFrom":makeQuery(id+"F5.opPattern","COPY",BODY,{"derivedFrom":makeQuery(id+"F4.opPattern","COPY",BODY,{"derivedFrom":makeQuery(id+"F2.opPattern","COPY",BODY,{"derivedFrom":makeQuery(id+"F1.opRevolve","SWEPT_BODY",BODY,{"disambiguationData":[OSD([sQuery(id+"F0.wireOp",EDGE,"E1")])]}),"instanceName":"1"}),"instanceName":"1"}),"instanceName":"1"}),"instanceName":"1"}),"instanceName":"1"}),"instanceName":"1"});
            var Q431;
            Q431=makeQuery(id+"F11.opPattern","COPY",BODY,{"derivedFrom":makeQuery(id+"F7.opPattern","COPY",BODY,{"derivedFrom":makeQuery(id+"F6.opPattern","COPY",BODY,{"derivedFrom":makeQuery(id+"F5.opPattern","COPY",BODY,{"derivedFrom":makeQuery(id+"F4.opPattern","COPY",BODY,{"derivedFrom":makeQuery(id+"F3.opPattern","COPY",BODY,{"derivedFrom":makeQuery(id+"F2.opPattern","COPY",BODY,{"derivedFrom":makeQuery(id+"F1.opRevolve","SWEPT_BODY",BODY,{"disambiguationData":[OSD([sQuery(id+"F0.wireOp",EDGE,"E1")])]}),"instanceName":"1"}),"instanceName":"1"}),"instanceName":"1"}),"instanceName":"1"}),"instanceName":"1"}),"instanceName":"1"}),"instanceName":"1"});
            var Q432;
            Q432=makeQuery(id+"F11.opPattern","COPY",BODY,{"derivedFrom":makeQuery(id+"F8.opPattern","COPY",BODY,{"derivedFrom":makeQuery(id+"F1.opRevolve","SWEPT_BODY",BODY,{"disambiguationData":[OSD([sQuery(id+"F0.wireOp",EDGE,"E1")])]}),"instanceName":"1"}),"instanceName":"1"});
            var Q433;
            Q433=makeQuery(id+"F11.opPattern","COPY",BODY,{"derivedFrom":makeQuery(id+"F8.opPattern","COPY",BODY,{"derivedFrom":makeQuery(id+"F2.opPattern","COPY",BODY,{"derivedFrom":makeQuery(id+"F1.opRevolve","SWEPT_BODY",BODY,{"disambiguationData":[OSD([sQuery(id+"F0.wireOp",EDGE,"E1")])]}),"instanceName":"1"}),"instanceName":"1"}),"instanceName":"1"});
            var Q434;
            Q434=makeQuery(id+"F11.opPattern","COPY",BODY,{"derivedFrom":makeQuery(id+"F8.opPattern","COPY",BODY,{"derivedFrom":makeQuery(id+"F3.opPattern","COPY",BODY,{"derivedFrom":makeQuery(id+"F2.opPattern","COPY",BODY,{"derivedFrom":makeQuery(id+"F1.opRevolve","SWEPT_BODY",BODY,{"disambiguationData":[OSD([sQuery(id+"F0.wireOp",EDGE,"E1")])]}),"instanceName":"1"}),"instanceName":"1"}),"instanceName":"1"}),"instanceName":"1"});
            var Q435;
            Q435=makeQuery(id+"F11.opPattern","COPY",BODY,{"derivedFrom":makeQuery(id+"F8.opPattern","COPY",BODY,{"derivedFrom":makeQuery(id+"F4.opPattern","COPY",BODY,{"derivedFrom":makeQuery(id+"F1.opRevolve","SWEPT_BODY",BODY,{"disambiguationData":[OSD([sQuery(id+"F0.wireOp",EDGE,"E1")])]}),"instanceName":"1"}),"instanceName":"1"}),"instanceName":"1"});
            var Q436;
            Q436=makeQuery(id+"F11.opPattern","COPY",BODY,{"derivedFrom":makeQuery(id+"F8.opPattern","COPY",BODY,{"derivedFrom":makeQuery(id+"F4.opPattern","COPY",BODY,{"derivedFrom":makeQuery(id+"F2.opPattern","COPY",BODY,{"derivedFrom":makeQuery(id+"F1.opRevolve","SWEPT_BODY",BODY,{"disambiguationData":[OSD([sQuery(id+"F0.wireOp",EDGE,"E1")])]}),"instanceName":"1"}),"instanceName":"1"}),"instanceName":"1"}),"instanceName":"1"});
            var Q437;
            Q437=makeQuery(id+"F11.opPattern","COPY",BODY,{"derivedFrom":makeQuery(id+"F8.opPattern","COPY",BODY,{"derivedFrom":makeQuery(id+"F4.opPattern","COPY",BODY,{"derivedFrom":makeQuery(id+"F3.opPattern","COPY",BODY,{"derivedFrom":makeQuery(id+"F2.opPattern","COPY",BODY,{"derivedFrom":makeQuery(id+"F1.opRevolve","SWEPT_BODY",BODY,{"disambiguationData":[OSD([sQuery(id+"F0.wireOp",EDGE,"E1")])]}),"instanceName":"1"}),"instanceName":"1"}),"instanceName":"1"}),"instanceName":"1"}),"instanceName":"1"});
            var Q438;
            Q438=makeQuery(id+"F11.opPattern","COPY",BODY,{"derivedFrom":makeQuery(id+"F8.opPattern","COPY",BODY,{"derivedFrom":makeQuery(id+"F5.opPattern","COPY",BODY,{"derivedFrom":makeQuery(id+"F1.opRevolve","SWEPT_BODY",BODY,{"disambiguationData":[OSD([sQuery(id+"F0.wireOp",EDGE,"E1")])]}),"instanceName":"1"}),"instanceName":"1"}),"instanceName":"1"});
            var Q439;
            Q439=makeQuery(id+"F11.opPattern","COPY",BODY,{"derivedFrom":makeQuery(id+"F8.opPattern","COPY",BODY,{"derivedFrom":makeQuery(id+"F5.opPattern","COPY",BODY,{"derivedFrom":makeQuery(id+"F2.opPattern","COPY",BODY,{"derivedFrom":makeQuery(id+"F1.opRevolve","SWEPT_BODY",BODY,{"disambiguationData":[OSD([sQuery(id+"F0.wireOp",EDGE,"E1")])]}),"instanceName":"1"}),"instanceName":"1"}),"instanceName":"1"}),"instanceName":"1"});
            var Q440;
            Q440=makeQuery(id+"F11.opPattern","COPY",BODY,{"derivedFrom":makeQuery(id+"F8.opPattern","COPY",BODY,{"derivedFrom":makeQuery(id+"F5.opPattern","COPY",BODY,{"derivedFrom":makeQuery(id+"F3.opPattern","COPY",BODY,{"derivedFrom":makeQuery(id+"F2.opPattern","COPY",BODY,{"derivedFrom":makeQuery(id+"F1.opRevolve","SWEPT_BODY",BODY,{"disambiguationData":[OSD([sQuery(id+"F0.wireOp",EDGE,"E1")])]}),"instanceName":"1"}),"instanceName":"1"}),"instanceName":"1"}),"instanceName":"1"}),"instanceName":"1"});
            var Q441;
            Q441=makeQuery(id+"F11.opPattern","COPY",BODY,{"derivedFrom":makeQuery(id+"F8.opPattern","COPY",BODY,{"derivedFrom":makeQuery(id+"F5.opPattern","COPY",BODY,{"derivedFrom":makeQuery(id+"F4.opPattern","COPY",BODY,{"derivedFrom":makeQuery(id+"F1.opRevolve","SWEPT_BODY",BODY,{"disambiguationData":[OSD([sQuery(id+"F0.wireOp",EDGE,"E1")])]}),"instanceName":"1"}),"instanceName":"1"}),"instanceName":"1"}),"instanceName":"1"});
            var Q442;
            Q442=makeQuery(id+"F11.opPattern","COPY",BODY,{"derivedFrom":makeQuery(id+"F8.opPattern","COPY",BODY,{"derivedFrom":makeQuery(id+"F5.opPattern","COPY",BODY,{"derivedFrom":makeQuery(id+"F4.opPattern","COPY",BODY,{"derivedFrom":makeQuery(id+"F2.opPattern","COPY",BODY,{"derivedFrom":makeQuery(id+"F1.opRevolve","SWEPT_BODY",BODY,{"disambiguationData":[OSD([sQuery(id+"F0.wireOp",EDGE,"E1")])]}),"instanceName":"1"}),"instanceName":"1"}),"instanceName":"1"}),"instanceName":"1"}),"instanceName":"1"});
            var Q443;
            Q443=makeQuery(id+"F11.opPattern","COPY",BODY,{"derivedFrom":makeQuery(id+"F8.opPattern","COPY",BODY,{"derivedFrom":makeQuery(id+"F5.opPattern","COPY",BODY,{"derivedFrom":makeQuery(id+"F4.opPattern","COPY",BODY,{"derivedFrom":makeQuery(id+"F3.opPattern","COPY",BODY,{"derivedFrom":makeQuery(id+"F2.opPattern","COPY",BODY,{"derivedFrom":makeQuery(id+"F1.opRevolve","SWEPT_BODY",BODY,{"disambiguationData":[OSD([sQuery(id+"F0.wireOp",EDGE,"E1")])]}),"instanceName":"1"}),"instanceName":"1"}),"instanceName":"1"}),"instanceName":"1"}),"instanceName":"1"}),"instanceName":"1"});
            var Q444;
            Q444=makeQuery(id+"F11.opPattern","COPY",BODY,{"derivedFrom":makeQuery(id+"F8.opPattern","COPY",BODY,{"derivedFrom":makeQuery(id+"F6.opPattern","COPY",BODY,{"derivedFrom":makeQuery(id+"F1.opRevolve","SWEPT_BODY",BODY,{"disambiguationData":[OSD([sQuery(id+"F0.wireOp",EDGE,"E1")])]}),"instanceName":"1"}),"instanceName":"1"}),"instanceName":"1"});
            var Q445;
            Q445=makeQuery(id+"F11.opPattern","COPY",BODY,{"derivedFrom":makeQuery(id+"F8.opPattern","COPY",BODY,{"derivedFrom":makeQuery(id+"F6.opPattern","COPY",BODY,{"derivedFrom":makeQuery(id+"F2.opPattern","COPY",BODY,{"derivedFrom":makeQuery(id+"F1.opRevolve","SWEPT_BODY",BODY,{"disambiguationData":[OSD([sQuery(id+"F0.wireOp",EDGE,"E1")])]}),"instanceName":"1"}),"instanceName":"1"}),"instanceName":"1"}),"instanceName":"1"});
            var Q446;
            Q446=makeQuery(id+"F11.opPattern","COPY",BODY,{"derivedFrom":makeQuery(id+"F8.opPattern","COPY",BODY,{"derivedFrom":makeQuery(id+"F6.opPattern","COPY",BODY,{"derivedFrom":makeQuery(id+"F3.opPattern","COPY",BODY,{"derivedFrom":makeQuery(id+"F2.opPattern","COPY",BODY,{"derivedFrom":makeQuery(id+"F1.opRevolve","SWEPT_BODY",BODY,{"disambiguationData":[OSD([sQuery(id+"F0.wireOp",EDGE,"E1")])]}),"instanceName":"1"}),"instanceName":"1"}),"instanceName":"1"}),"instanceName":"1"}),"instanceName":"1"});
            var Q447;
            Q447=makeQuery(id+"F11.opPattern","COPY",BODY,{"derivedFrom":makeQuery(id+"F8.opPattern","COPY",BODY,{"derivedFrom":makeQuery(id+"F6.opPattern","COPY",BODY,{"derivedFrom":makeQuery(id+"F4.opPattern","COPY",BODY,{"derivedFrom":makeQuery(id+"F1.opRevolve","SWEPT_BODY",BODY,{"disambiguationData":[OSD([sQuery(id+"F0.wireOp",EDGE,"E1")])]}),"instanceName":"1"}),"instanceName":"1"}),"instanceName":"1"}),"instanceName":"1"});
            var Q448;
            Q448=makeQuery(id+"F11.opPattern","COPY",BODY,{"derivedFrom":makeQuery(id+"F8.opPattern","COPY",BODY,{"derivedFrom":makeQuery(id+"F6.opPattern","COPY",BODY,{"derivedFrom":makeQuery(id+"F4.opPattern","COPY",BODY,{"derivedFrom":makeQuery(id+"F2.opPattern","COPY",BODY,{"derivedFrom":makeQuery(id+"F1.opRevolve","SWEPT_BODY",BODY,{"disambiguationData":[OSD([sQuery(id+"F0.wireOp",EDGE,"E1")])]}),"instanceName":"1"}),"instanceName":"1"}),"instanceName":"1"}),"instanceName":"1"}),"instanceName":"1"});
            var Q449;
            Q449=makeQuery(id+"F11.opPattern","COPY",BODY,{"derivedFrom":makeQuery(id+"F8.opPattern","COPY",BODY,{"derivedFrom":makeQuery(id+"F6.opPattern","COPY",BODY,{"derivedFrom":makeQuery(id+"F4.opPattern","COPY",BODY,{"derivedFrom":makeQuery(id+"F3.opPattern","COPY",BODY,{"derivedFrom":makeQuery(id+"F2.opPattern","COPY",BODY,{"derivedFrom":makeQuery(id+"F1.opRevolve","SWEPT_BODY",BODY,{"disambiguationData":[OSD([sQuery(id+"F0.wireOp",EDGE,"E1")])]}),"instanceName":"1"}),"instanceName":"1"}),"instanceName":"1"}),"instanceName":"1"}),"instanceName":"1"}),"instanceName":"1"});
            var Q450;
            Q450=makeQuery(id+"F11.opPattern","COPY",BODY,{"derivedFrom":makeQuery(id+"F8.opPattern","COPY",BODY,{"derivedFrom":makeQuery(id+"F6.opPattern","COPY",BODY,{"derivedFrom":makeQuery(id+"F5.opPattern","COPY",BODY,{"derivedFrom":makeQuery(id+"F1.opRevolve","SWEPT_BODY",BODY,{"disambiguationData":[OSD([sQuery(id+"F0.wireOp",EDGE,"E1")])]}),"instanceName":"1"}),"instanceName":"1"}),"instanceName":"1"}),"instanceName":"1"});
            var Q451;
            Q451=makeQuery(id+"F11.opPattern","COPY",BODY,{"derivedFrom":makeQuery(id+"F8.opPattern","COPY",BODY,{"derivedFrom":makeQuery(id+"F6.opPattern","COPY",BODY,{"derivedFrom":makeQuery(id+"F5.opPattern","COPY",BODY,{"derivedFrom":makeQuery(id+"F2.opPattern","COPY",BODY,{"derivedFrom":makeQuery(id+"F1.opRevolve","SWEPT_BODY",BODY,{"disambiguationData":[OSD([sQuery(id+"F0.wireOp",EDGE,"E1")])]}),"instanceName":"1"}),"instanceName":"1"}),"instanceName":"1"}),"instanceName":"1"}),"instanceName":"1"});
            var Q452;
            Q452=makeQuery(id+"F11.opPattern","COPY",BODY,{"derivedFrom":makeQuery(id+"F8.opPattern","COPY",BODY,{"derivedFrom":makeQuery(id+"F6.opPattern","COPY",BODY,{"derivedFrom":makeQuery(id+"F5.opPattern","COPY",BODY,{"derivedFrom":makeQuery(id+"F3.opPattern","COPY",BODY,{"derivedFrom":makeQuery(id+"F2.opPattern","COPY",BODY,{"derivedFrom":makeQuery(id+"F1.opRevolve","SWEPT_BODY",BODY,{"disambiguationData":[OSD([sQuery(id+"F0.wireOp",EDGE,"E1")])]}),"instanceName":"1"}),"instanceName":"1"}),"instanceName":"1"}),"instanceName":"1"}),"instanceName":"1"}),"instanceName":"1"});
            var Q453;
            Q453=makeQuery(id+"F11.opPattern","COPY",BODY,{"derivedFrom":makeQuery(id+"F8.opPattern","COPY",BODY,{"derivedFrom":makeQuery(id+"F6.opPattern","COPY",BODY,{"derivedFrom":makeQuery(id+"F5.opPattern","COPY",BODY,{"derivedFrom":makeQuery(id+"F4.opPattern","COPY",BODY,{"derivedFrom":makeQuery(id+"F1.opRevolve","SWEPT_BODY",BODY,{"disambiguationData":[OSD([sQuery(id+"F0.wireOp",EDGE,"E1")])]}),"instanceName":"1"}),"instanceName":"1"}),"instanceName":"1"}),"instanceName":"1"}),"instanceName":"1"});
            var Q454;
            Q454=makeQuery(id+"F11.opPattern","COPY",BODY,{"derivedFrom":makeQuery(id+"F8.opPattern","COPY",BODY,{"derivedFrom":makeQuery(id+"F6.opPattern","COPY",BODY,{"derivedFrom":makeQuery(id+"F5.opPattern","COPY",BODY,{"derivedFrom":makeQuery(id+"F4.opPattern","COPY",BODY,{"derivedFrom":makeQuery(id+"F2.opPattern","COPY",BODY,{"derivedFrom":makeQuery(id+"F1.opRevolve","SWEPT_BODY",BODY,{"disambiguationData":[OSD([sQuery(id+"F0.wireOp",EDGE,"E1")])]}),"instanceName":"1"}),"instanceName":"1"}),"instanceName":"1"}),"instanceName":"1"}),"instanceName":"1"}),"instanceName":"1"});
            var Q455;
            Q455=makeQuery(id+"F11.opPattern","COPY",BODY,{"derivedFrom":makeQuery(id+"F8.opPattern","COPY",BODY,{"derivedFrom":makeQuery(id+"F6.opPattern","COPY",BODY,{"derivedFrom":makeQuery(id+"F5.opPattern","COPY",BODY,{"derivedFrom":makeQuery(id+"F4.opPattern","COPY",BODY,{"derivedFrom":makeQuery(id+"F3.opPattern","COPY",BODY,{"derivedFrom":makeQuery(id+"F2.opPattern","COPY",BODY,{"derivedFrom":makeQuery(id+"F1.opRevolve","SWEPT_BODY",BODY,{"disambiguationData":[OSD([sQuery(id+"F0.wireOp",EDGE,"E1")])]}),"instanceName":"1"}),"instanceName":"1"}),"instanceName":"1"}),"instanceName":"1"}),"instanceName":"1"}),"instanceName":"1"}),"instanceName":"1"});
            var Q456;
            Q456=makeQuery(id+"F11.opPattern","COPY",BODY,{"derivedFrom":makeQuery(id+"F8.opPattern","COPY",BODY,{"derivedFrom":makeQuery(id+"F7.opPattern","COPY",BODY,{"derivedFrom":makeQuery(id+"F1.opRevolve","SWEPT_BODY",BODY,{"disambiguationData":[OSD([sQuery(id+"F0.wireOp",EDGE,"E1")])]}),"instanceName":"1"}),"instanceName":"1"}),"instanceName":"1"});
            var Q457;
            Q457=makeQuery(id+"F11.opPattern","COPY",BODY,{"derivedFrom":makeQuery(id+"F8.opPattern","COPY",BODY,{"derivedFrom":makeQuery(id+"F7.opPattern","COPY",BODY,{"derivedFrom":makeQuery(id+"F2.opPattern","COPY",BODY,{"derivedFrom":makeQuery(id+"F1.opRevolve","SWEPT_BODY",BODY,{"disambiguationData":[OSD([sQuery(id+"F0.wireOp",EDGE,"E1")])]}),"instanceName":"1"}),"instanceName":"1"}),"instanceName":"1"}),"instanceName":"1"});
            var Q458;
            Q458=makeQuery(id+"F11.opPattern","COPY",BODY,{"derivedFrom":makeQuery(id+"F8.opPattern","COPY",BODY,{"derivedFrom":makeQuery(id+"F7.opPattern","COPY",BODY,{"derivedFrom":makeQuery(id+"F3.opPattern","COPY",BODY,{"derivedFrom":makeQuery(id+"F2.opPattern","COPY",BODY,{"derivedFrom":makeQuery(id+"F1.opRevolve","SWEPT_BODY",BODY,{"disambiguationData":[OSD([sQuery(id+"F0.wireOp",EDGE,"E1")])]}),"instanceName":"1"}),"instanceName":"1"}),"instanceName":"1"}),"instanceName":"1"}),"instanceName":"1"});
            var Q459;
            Q459=makeQuery(id+"F11.opPattern","COPY",BODY,{"derivedFrom":makeQuery(id+"F8.opPattern","COPY",BODY,{"derivedFrom":makeQuery(id+"F7.opPattern","COPY",BODY,{"derivedFrom":makeQuery(id+"F4.opPattern","COPY",BODY,{"derivedFrom":makeQuery(id+"F1.opRevolve","SWEPT_BODY",BODY,{"disambiguationData":[OSD([sQuery(id+"F0.wireOp",EDGE,"E1")])]}),"instanceName":"1"}),"instanceName":"1"}),"instanceName":"1"}),"instanceName":"1"});
            var Q460;
            Q460=makeQuery(id+"F11.opPattern","COPY",BODY,{"derivedFrom":makeQuery(id+"F8.opPattern","COPY",BODY,{"derivedFrom":makeQuery(id+"F7.opPattern","COPY",BODY,{"derivedFrom":makeQuery(id+"F4.opPattern","COPY",BODY,{"derivedFrom":makeQuery(id+"F2.opPattern","COPY",BODY,{"derivedFrom":makeQuery(id+"F1.opRevolve","SWEPT_BODY",BODY,{"disambiguationData":[OSD([sQuery(id+"F0.wireOp",EDGE,"E1")])]}),"instanceName":"1"}),"instanceName":"1"}),"instanceName":"1"}),"instanceName":"1"}),"instanceName":"1"});
            var Q461;
            Q461=makeQuery(id+"F11.opPattern","COPY",BODY,{"derivedFrom":makeQuery(id+"F8.opPattern","COPY",BODY,{"derivedFrom":makeQuery(id+"F7.opPattern","COPY",BODY,{"derivedFrom":makeQuery(id+"F4.opPattern","COPY",BODY,{"derivedFrom":makeQuery(id+"F3.opPattern","COPY",BODY,{"derivedFrom":makeQuery(id+"F2.opPattern","COPY",BODY,{"derivedFrom":makeQuery(id+"F1.opRevolve","SWEPT_BODY",BODY,{"disambiguationData":[OSD([sQuery(id+"F0.wireOp",EDGE,"E1")])]}),"instanceName":"1"}),"instanceName":"1"}),"instanceName":"1"}),"instanceName":"1"}),"instanceName":"1"}),"instanceName":"1"});
            var Q462;
            Q462=makeQuery(id+"F11.opPattern","COPY",BODY,{"derivedFrom":makeQuery(id+"F8.opPattern","COPY",BODY,{"derivedFrom":makeQuery(id+"F7.opPattern","COPY",BODY,{"derivedFrom":makeQuery(id+"F5.opPattern","COPY",BODY,{"derivedFrom":makeQuery(id+"F1.opRevolve","SWEPT_BODY",BODY,{"disambiguationData":[OSD([sQuery(id+"F0.wireOp",EDGE,"E1")])]}),"instanceName":"1"}),"instanceName":"1"}),"instanceName":"1"}),"instanceName":"1"});
            var Q463;
            Q463=makeQuery(id+"F11.opPattern","COPY",BODY,{"derivedFrom":makeQuery(id+"F8.opPattern","COPY",BODY,{"derivedFrom":makeQuery(id+"F7.opPattern","COPY",BODY,{"derivedFrom":makeQuery(id+"F5.opPattern","COPY",BODY,{"derivedFrom":makeQuery(id+"F2.opPattern","COPY",BODY,{"derivedFrom":makeQuery(id+"F1.opRevolve","SWEPT_BODY",BODY,{"disambiguationData":[OSD([sQuery(id+"F0.wireOp",EDGE,"E1")])]}),"instanceName":"1"}),"instanceName":"1"}),"instanceName":"1"}),"instanceName":"1"}),"instanceName":"1"});
            var Q464;
            Q464=makeQuery(id+"F11.opPattern","COPY",BODY,{"derivedFrom":makeQuery(id+"F8.opPattern","COPY",BODY,{"derivedFrom":makeQuery(id+"F7.opPattern","COPY",BODY,{"derivedFrom":makeQuery(id+"F5.opPattern","COPY",BODY,{"derivedFrom":makeQuery(id+"F3.opPattern","COPY",BODY,{"derivedFrom":makeQuery(id+"F2.opPattern","COPY",BODY,{"derivedFrom":makeQuery(id+"F1.opRevolve","SWEPT_BODY",BODY,{"disambiguationData":[OSD([sQuery(id+"F0.wireOp",EDGE,"E1")])]}),"instanceName":"1"}),"instanceName":"1"}),"instanceName":"1"}),"instanceName":"1"}),"instanceName":"1"}),"instanceName":"1"});
            var Q465;
            Q465=makeQuery(id+"F11.opPattern","COPY",BODY,{"derivedFrom":makeQuery(id+"F8.opPattern","COPY",BODY,{"derivedFrom":makeQuery(id+"F7.opPattern","COPY",BODY,{"derivedFrom":makeQuery(id+"F5.opPattern","COPY",BODY,{"derivedFrom":makeQuery(id+"F4.opPattern","COPY",BODY,{"derivedFrom":makeQuery(id+"F1.opRevolve","SWEPT_BODY",BODY,{"disambiguationData":[OSD([sQuery(id+"F0.wireOp",EDGE,"E1")])]}),"instanceName":"1"}),"instanceName":"1"}),"instanceName":"1"}),"instanceName":"1"}),"instanceName":"1"});
            var Q466;
            Q466=makeQuery(id+"F11.opPattern","COPY",BODY,{"derivedFrom":makeQuery(id+"F8.opPattern","COPY",BODY,{"derivedFrom":makeQuery(id+"F7.opPattern","COPY",BODY,{"derivedFrom":makeQuery(id+"F5.opPattern","COPY",BODY,{"derivedFrom":makeQuery(id+"F4.opPattern","COPY",BODY,{"derivedFrom":makeQuery(id+"F2.opPattern","COPY",BODY,{"derivedFrom":makeQuery(id+"F1.opRevolve","SWEPT_BODY",BODY,{"disambiguationData":[OSD([sQuery(id+"F0.wireOp",EDGE,"E1")])]}),"instanceName":"1"}),"instanceName":"1"}),"instanceName":"1"}),"instanceName":"1"}),"instanceName":"1"}),"instanceName":"1"});
            var Q467;
            Q467=makeQuery(id+"F11.opPattern","COPY",BODY,{"derivedFrom":makeQuery(id+"F8.opPattern","COPY",BODY,{"derivedFrom":makeQuery(id+"F7.opPattern","COPY",BODY,{"derivedFrom":makeQuery(id+"F5.opPattern","COPY",BODY,{"derivedFrom":makeQuery(id+"F4.opPattern","COPY",BODY,{"derivedFrom":makeQuery(id+"F3.opPattern","COPY",BODY,{"derivedFrom":makeQuery(id+"F2.opPattern","COPY",BODY,{"derivedFrom":makeQuery(id+"F1.opRevolve","SWEPT_BODY",BODY,{"disambiguationData":[OSD([sQuery(id+"F0.wireOp",EDGE,"E1")])]}),"instanceName":"1"}),"instanceName":"1"}),"instanceName":"1"}),"instanceName":"1"}),"instanceName":"1"}),"instanceName":"1"}),"instanceName":"1"});
            var Q468;
            Q468=makeQuery(id+"F11.opPattern","COPY",BODY,{"derivedFrom":makeQuery(id+"F8.opPattern","COPY",BODY,{"derivedFrom":makeQuery(id+"F7.opPattern","COPY",BODY,{"derivedFrom":makeQuery(id+"F6.opPattern","COPY",BODY,{"derivedFrom":makeQuery(id+"F1.opRevolve","SWEPT_BODY",BODY,{"disambiguationData":[OSD([sQuery(id+"F0.wireOp",EDGE,"E1")])]}),"instanceName":"1"}),"instanceName":"1"}),"instanceName":"1"}),"instanceName":"1"});
            var Q469;
            Q469=makeQuery(id+"F11.opPattern","COPY",BODY,{"derivedFrom":makeQuery(id+"F8.opPattern","COPY",BODY,{"derivedFrom":makeQuery(id+"F7.opPattern","COPY",BODY,{"derivedFrom":makeQuery(id+"F6.opPattern","COPY",BODY,{"derivedFrom":makeQuery(id+"F2.opPattern","COPY",BODY,{"derivedFrom":makeQuery(id+"F1.opRevolve","SWEPT_BODY",BODY,{"disambiguationData":[OSD([sQuery(id+"F0.wireOp",EDGE,"E1")])]}),"instanceName":"1"}),"instanceName":"1"}),"instanceName":"1"}),"instanceName":"1"}),"instanceName":"1"});
            var Q470;
            Q470=makeQuery(id+"F11.opPattern","COPY",BODY,{"derivedFrom":makeQuery(id+"F8.opPattern","COPY",BODY,{"derivedFrom":makeQuery(id+"F7.opPattern","COPY",BODY,{"derivedFrom":makeQuery(id+"F6.opPattern","COPY",BODY,{"derivedFrom":makeQuery(id+"F3.opPattern","COPY",BODY,{"derivedFrom":makeQuery(id+"F2.opPattern","COPY",BODY,{"derivedFrom":makeQuery(id+"F1.opRevolve","SWEPT_BODY",BODY,{"disambiguationData":[OSD([sQuery(id+"F0.wireOp",EDGE,"E1")])]}),"instanceName":"1"}),"instanceName":"1"}),"instanceName":"1"}),"instanceName":"1"}),"instanceName":"1"}),"instanceName":"1"});
            var Q471;
            Q471=makeQuery(id+"F11.opPattern","COPY",BODY,{"derivedFrom":makeQuery(id+"F8.opPattern","COPY",BODY,{"derivedFrom":makeQuery(id+"F7.opPattern","COPY",BODY,{"derivedFrom":makeQuery(id+"F6.opPattern","COPY",BODY,{"derivedFrom":makeQuery(id+"F4.opPattern","COPY",BODY,{"derivedFrom":makeQuery(id+"F1.opRevolve","SWEPT_BODY",BODY,{"disambiguationData":[OSD([sQuery(id+"F0.wireOp",EDGE,"E1")])]}),"instanceName":"1"}),"instanceName":"1"}),"instanceName":"1"}),"instanceName":"1"}),"instanceName":"1"});
            var Q472;
            Q472=makeQuery(id+"F11.opPattern","COPY",BODY,{"derivedFrom":makeQuery(id+"F8.opPattern","COPY",BODY,{"derivedFrom":makeQuery(id+"F7.opPattern","COPY",BODY,{"derivedFrom":makeQuery(id+"F6.opPattern","COPY",BODY,{"derivedFrom":makeQuery(id+"F4.opPattern","COPY",BODY,{"derivedFrom":makeQuery(id+"F2.opPattern","COPY",BODY,{"derivedFrom":makeQuery(id+"F1.opRevolve","SWEPT_BODY",BODY,{"disambiguationData":[OSD([sQuery(id+"F0.wireOp",EDGE,"E1")])]}),"instanceName":"1"}),"instanceName":"1"}),"instanceName":"1"}),"instanceName":"1"}),"instanceName":"1"}),"instanceName":"1"});
            var Q473;
            Q473=makeQuery(id+"F11.opPattern","COPY",BODY,{"derivedFrom":makeQuery(id+"F8.opPattern","COPY",BODY,{"derivedFrom":makeQuery(id+"F7.opPattern","COPY",BODY,{"derivedFrom":makeQuery(id+"F6.opPattern","COPY",BODY,{"derivedFrom":makeQuery(id+"F4.opPattern","COPY",BODY,{"derivedFrom":makeQuery(id+"F3.opPattern","COPY",BODY,{"derivedFrom":makeQuery(id+"F2.opPattern","COPY",BODY,{"derivedFrom":makeQuery(id+"F1.opRevolve","SWEPT_BODY",BODY,{"disambiguationData":[OSD([sQuery(id+"F0.wireOp",EDGE,"E1")])]}),"instanceName":"1"}),"instanceName":"1"}),"instanceName":"1"}),"instanceName":"1"}),"instanceName":"1"}),"instanceName":"1"}),"instanceName":"1"});
            var Q474;
            Q474=makeQuery(id+"F11.opPattern","COPY",BODY,{"derivedFrom":makeQuery(id+"F8.opPattern","COPY",BODY,{"derivedFrom":makeQuery(id+"F7.opPattern","COPY",BODY,{"derivedFrom":makeQuery(id+"F6.opPattern","COPY",BODY,{"derivedFrom":makeQuery(id+"F5.opPattern","COPY",BODY,{"derivedFrom":makeQuery(id+"F1.opRevolve","SWEPT_BODY",BODY,{"disambiguationData":[OSD([sQuery(id+"F0.wireOp",EDGE,"E1")])]}),"instanceName":"1"}),"instanceName":"1"}),"instanceName":"1"}),"instanceName":"1"}),"instanceName":"1"});
            var Q475;
            Q475=makeQuery(id+"F11.opPattern","COPY",BODY,{"derivedFrom":makeQuery(id+"F8.opPattern","COPY",BODY,{"derivedFrom":makeQuery(id+"F7.opPattern","COPY",BODY,{"derivedFrom":makeQuery(id+"F6.opPattern","COPY",BODY,{"derivedFrom":makeQuery(id+"F5.opPattern","COPY",BODY,{"derivedFrom":makeQuery(id+"F2.opPattern","COPY",BODY,{"derivedFrom":makeQuery(id+"F1.opRevolve","SWEPT_BODY",BODY,{"disambiguationData":[OSD([sQuery(id+"F0.wireOp",EDGE,"E1")])]}),"instanceName":"1"}),"instanceName":"1"}),"instanceName":"1"}),"instanceName":"1"}),"instanceName":"1"}),"instanceName":"1"});
            var Q476;
            Q476=makeQuery(id+"F11.opPattern","COPY",BODY,{"derivedFrom":makeQuery(id+"F8.opPattern","COPY",BODY,{"derivedFrom":makeQuery(id+"F7.opPattern","COPY",BODY,{"derivedFrom":makeQuery(id+"F6.opPattern","COPY",BODY,{"derivedFrom":makeQuery(id+"F5.opPattern","COPY",BODY,{"derivedFrom":makeQuery(id+"F3.opPattern","COPY",BODY,{"derivedFrom":makeQuery(id+"F2.opPattern","COPY",BODY,{"derivedFrom":makeQuery(id+"F1.opRevolve","SWEPT_BODY",BODY,{"disambiguationData":[OSD([sQuery(id+"F0.wireOp",EDGE,"E1")])]}),"instanceName":"1"}),"instanceName":"1"}),"instanceName":"1"}),"instanceName":"1"}),"instanceName":"1"}),"instanceName":"1"}),"instanceName":"1"});
            var Q477;
            Q477=makeQuery(id+"F11.opPattern","COPY",BODY,{"derivedFrom":makeQuery(id+"F8.opPattern","COPY",BODY,{"derivedFrom":makeQuery(id+"F7.opPattern","COPY",BODY,{"derivedFrom":makeQuery(id+"F6.opPattern","COPY",BODY,{"derivedFrom":makeQuery(id+"F5.opPattern","COPY",BODY,{"derivedFrom":makeQuery(id+"F4.opPattern","COPY",BODY,{"derivedFrom":makeQuery(id+"F1.opRevolve","SWEPT_BODY",BODY,{"disambiguationData":[OSD([sQuery(id+"F0.wireOp",EDGE,"E1")])]}),"instanceName":"1"}),"instanceName":"1"}),"instanceName":"1"}),"instanceName":"1"}),"instanceName":"1"}),"instanceName":"1"});
            var Q478;
            Q478=makeQuery(id+"F11.opPattern","COPY",BODY,{"derivedFrom":makeQuery(id+"F8.opPattern","COPY",BODY,{"derivedFrom":makeQuery(id+"F7.opPattern","COPY",BODY,{"derivedFrom":makeQuery(id+"F6.opPattern","COPY",BODY,{"derivedFrom":makeQuery(id+"F5.opPattern","COPY",BODY,{"derivedFrom":makeQuery(id+"F4.opPattern","COPY",BODY,{"derivedFrom":makeQuery(id+"F2.opPattern","COPY",BODY,{"derivedFrom":makeQuery(id+"F1.opRevolve","SWEPT_BODY",BODY,{"disambiguationData":[OSD([sQuery(id+"F0.wireOp",EDGE,"E1")])]}),"instanceName":"1"}),"instanceName":"1"}),"instanceName":"1"}),"instanceName":"1"}),"instanceName":"1"}),"instanceName":"1"}),"instanceName":"1"});
            var Q479;
            Q479=makeQuery(id+"F11.opPattern","COPY",BODY,{"derivedFrom":makeQuery(id+"F8.opPattern","COPY",BODY,{"derivedFrom":makeQuery(id+"F7.opPattern","COPY",BODY,{"derivedFrom":makeQuery(id+"F6.opPattern","COPY",BODY,{"derivedFrom":makeQuery(id+"F5.opPattern","COPY",BODY,{"derivedFrom":makeQuery(id+"F4.opPattern","COPY",BODY,{"derivedFrom":makeQuery(id+"F3.opPattern","COPY",BODY,{"derivedFrom":makeQuery(id+"F2.opPattern","COPY",BODY,{"derivedFrom":makeQuery(id+"F1.opRevolve","SWEPT_BODY",BODY,{"disambiguationData":[OSD([sQuery(id+"F0.wireOp",EDGE,"E1")])]}),"instanceName":"1"}),"instanceName":"1"}),"instanceName":"1"}),"instanceName":"1"}),"instanceName":"1"}),"instanceName":"1"}),"instanceName":"1"}),"instanceName":"1"});
            var Q480;
            Q480=makeQuery(id+"F11.opPattern","COPY",BODY,{"derivedFrom":makeQuery(id+"F9.opPattern","COPY",BODY,{"derivedFrom":makeQuery(id+"F1.opRevolve","SWEPT_BODY",BODY,{"disambiguationData":[OSD([sQuery(id+"F0.wireOp",EDGE,"E1")])]}),"instanceName":"1"}),"instanceName":"1"});
            var Q481;
            Q481=makeQuery(id+"F11.opPattern","COPY",BODY,{"derivedFrom":makeQuery(id+"F9.opPattern","COPY",BODY,{"derivedFrom":makeQuery(id+"F2.opPattern","COPY",BODY,{"derivedFrom":makeQuery(id+"F1.opRevolve","SWEPT_BODY",BODY,{"disambiguationData":[OSD([sQuery(id+"F0.wireOp",EDGE,"E1")])]}),"instanceName":"1"}),"instanceName":"1"}),"instanceName":"1"});
            var Q482;
            Q482=makeQuery(id+"F11.opPattern","COPY",BODY,{"derivedFrom":makeQuery(id+"F9.opPattern","COPY",BODY,{"derivedFrom":makeQuery(id+"F3.opPattern","COPY",BODY,{"derivedFrom":makeQuery(id+"F2.opPattern","COPY",BODY,{"derivedFrom":makeQuery(id+"F1.opRevolve","SWEPT_BODY",BODY,{"disambiguationData":[OSD([sQuery(id+"F0.wireOp",EDGE,"E1")])]}),"instanceName":"1"}),"instanceName":"1"}),"instanceName":"1"}),"instanceName":"1"});
            var Q483;
            Q483=makeQuery(id+"F11.opPattern","COPY",BODY,{"derivedFrom":makeQuery(id+"F9.opPattern","COPY",BODY,{"derivedFrom":makeQuery(id+"F4.opPattern","COPY",BODY,{"derivedFrom":makeQuery(id+"F1.opRevolve","SWEPT_BODY",BODY,{"disambiguationData":[OSD([sQuery(id+"F0.wireOp",EDGE,"E1")])]}),"instanceName":"1"}),"instanceName":"1"}),"instanceName":"1"});
            var Q484;
            Q484=makeQuery(id+"F11.opPattern","COPY",BODY,{"derivedFrom":makeQuery(id+"F9.opPattern","COPY",BODY,{"derivedFrom":makeQuery(id+"F4.opPattern","COPY",BODY,{"derivedFrom":makeQuery(id+"F2.opPattern","COPY",BODY,{"derivedFrom":makeQuery(id+"F1.opRevolve","SWEPT_BODY",BODY,{"disambiguationData":[OSD([sQuery(id+"F0.wireOp",EDGE,"E1")])]}),"instanceName":"1"}),"instanceName":"1"}),"instanceName":"1"}),"instanceName":"1"});
            var Q485;
            Q485=makeQuery(id+"F11.opPattern","COPY",BODY,{"derivedFrom":makeQuery(id+"F9.opPattern","COPY",BODY,{"derivedFrom":makeQuery(id+"F4.opPattern","COPY",BODY,{"derivedFrom":makeQuery(id+"F3.opPattern","COPY",BODY,{"derivedFrom":makeQuery(id+"F2.opPattern","COPY",BODY,{"derivedFrom":makeQuery(id+"F1.opRevolve","SWEPT_BODY",BODY,{"disambiguationData":[OSD([sQuery(id+"F0.wireOp",EDGE,"E1")])]}),"instanceName":"1"}),"instanceName":"1"}),"instanceName":"1"}),"instanceName":"1"}),"instanceName":"1"});
            var Q486;
            Q486=makeQuery(id+"F11.opPattern","COPY",BODY,{"derivedFrom":makeQuery(id+"F9.opPattern","COPY",BODY,{"derivedFrom":makeQuery(id+"F5.opPattern","COPY",BODY,{"derivedFrom":makeQuery(id+"F1.opRevolve","SWEPT_BODY",BODY,{"disambiguationData":[OSD([sQuery(id+"F0.wireOp",EDGE,"E1")])]}),"instanceName":"1"}),"instanceName":"1"}),"instanceName":"1"});
            var Q487;
            Q487=makeQuery(id+"F11.opPattern","COPY",BODY,{"derivedFrom":makeQuery(id+"F9.opPattern","COPY",BODY,{"derivedFrom":makeQuery(id+"F5.opPattern","COPY",BODY,{"derivedFrom":makeQuery(id+"F2.opPattern","COPY",BODY,{"derivedFrom":makeQuery(id+"F1.opRevolve","SWEPT_BODY",BODY,{"disambiguationData":[OSD([sQuery(id+"F0.wireOp",EDGE,"E1")])]}),"instanceName":"1"}),"instanceName":"1"}),"instanceName":"1"}),"instanceName":"1"});
            var Q488;
            Q488=makeQuery(id+"F11.opPattern","COPY",BODY,{"derivedFrom":makeQuery(id+"F9.opPattern","COPY",BODY,{"derivedFrom":makeQuery(id+"F5.opPattern","COPY",BODY,{"derivedFrom":makeQuery(id+"F3.opPattern","COPY",BODY,{"derivedFrom":makeQuery(id+"F2.opPattern","COPY",BODY,{"derivedFrom":makeQuery(id+"F1.opRevolve","SWEPT_BODY",BODY,{"disambiguationData":[OSD([sQuery(id+"F0.wireOp",EDGE,"E1")])]}),"instanceName":"1"}),"instanceName":"1"}),"instanceName":"1"}),"instanceName":"1"}),"instanceName":"1"});
            var Q489;
            Q489=makeQuery(id+"F11.opPattern","COPY",BODY,{"derivedFrom":makeQuery(id+"F9.opPattern","COPY",BODY,{"derivedFrom":makeQuery(id+"F5.opPattern","COPY",BODY,{"derivedFrom":makeQuery(id+"F4.opPattern","COPY",BODY,{"derivedFrom":makeQuery(id+"F1.opRevolve","SWEPT_BODY",BODY,{"disambiguationData":[OSD([sQuery(id+"F0.wireOp",EDGE,"E1")])]}),"instanceName":"1"}),"instanceName":"1"}),"instanceName":"1"}),"instanceName":"1"});
            var Q490;
            Q490=makeQuery(id+"F11.opPattern","COPY",BODY,{"derivedFrom":makeQuery(id+"F9.opPattern","COPY",BODY,{"derivedFrom":makeQuery(id+"F5.opPattern","COPY",BODY,{"derivedFrom":makeQuery(id+"F4.opPattern","COPY",BODY,{"derivedFrom":makeQuery(id+"F2.opPattern","COPY",BODY,{"derivedFrom":makeQuery(id+"F1.opRevolve","SWEPT_BODY",BODY,{"disambiguationData":[OSD([sQuery(id+"F0.wireOp",EDGE,"E1")])]}),"instanceName":"1"}),"instanceName":"1"}),"instanceName":"1"}),"instanceName":"1"}),"instanceName":"1"});
            var Q491;
            Q491=makeQuery(id+"F11.opPattern","COPY",BODY,{"derivedFrom":makeQuery(id+"F9.opPattern","COPY",BODY,{"derivedFrom":makeQuery(id+"F5.opPattern","COPY",BODY,{"derivedFrom":makeQuery(id+"F4.opPattern","COPY",BODY,{"derivedFrom":makeQuery(id+"F3.opPattern","COPY",BODY,{"derivedFrom":makeQuery(id+"F2.opPattern","COPY",BODY,{"derivedFrom":makeQuery(id+"F1.opRevolve","SWEPT_BODY",BODY,{"disambiguationData":[OSD([sQuery(id+"F0.wireOp",EDGE,"E1")])]}),"instanceName":"1"}),"instanceName":"1"}),"instanceName":"1"}),"instanceName":"1"}),"instanceName":"1"}),"instanceName":"1"});
            var Q492;
            Q492=makeQuery(id+"F11.opPattern","COPY",BODY,{"derivedFrom":makeQuery(id+"F9.opPattern","COPY",BODY,{"derivedFrom":makeQuery(id+"F6.opPattern","COPY",BODY,{"derivedFrom":makeQuery(id+"F1.opRevolve","SWEPT_BODY",BODY,{"disambiguationData":[OSD([sQuery(id+"F0.wireOp",EDGE,"E1")])]}),"instanceName":"1"}),"instanceName":"1"}),"instanceName":"1"});
            var Q493;
            Q493=makeQuery(id+"F11.opPattern","COPY",BODY,{"derivedFrom":makeQuery(id+"F9.opPattern","COPY",BODY,{"derivedFrom":makeQuery(id+"F6.opPattern","COPY",BODY,{"derivedFrom":makeQuery(id+"F2.opPattern","COPY",BODY,{"derivedFrom":makeQuery(id+"F1.opRevolve","SWEPT_BODY",BODY,{"disambiguationData":[OSD([sQuery(id+"F0.wireOp",EDGE,"E1")])]}),"instanceName":"1"}),"instanceName":"1"}),"instanceName":"1"}),"instanceName":"1"});
            var Q494;
            Q494=makeQuery(id+"F11.opPattern","COPY",BODY,{"derivedFrom":makeQuery(id+"F9.opPattern","COPY",BODY,{"derivedFrom":makeQuery(id+"F6.opPattern","COPY",BODY,{"derivedFrom":makeQuery(id+"F3.opPattern","COPY",BODY,{"derivedFrom":makeQuery(id+"F2.opPattern","COPY",BODY,{"derivedFrom":makeQuery(id+"F1.opRevolve","SWEPT_BODY",BODY,{"disambiguationData":[OSD([sQuery(id+"F0.wireOp",EDGE,"E1")])]}),"instanceName":"1"}),"instanceName":"1"}),"instanceName":"1"}),"instanceName":"1"}),"instanceName":"1"});
            var Q495;
            Q495=makeQuery(id+"F11.opPattern","COPY",BODY,{"derivedFrom":makeQuery(id+"F9.opPattern","COPY",BODY,{"derivedFrom":makeQuery(id+"F6.opPattern","COPY",BODY,{"derivedFrom":makeQuery(id+"F4.opPattern","COPY",BODY,{"derivedFrom":makeQuery(id+"F1.opRevolve","SWEPT_BODY",BODY,{"disambiguationData":[OSD([sQuery(id+"F0.wireOp",EDGE,"E1")])]}),"instanceName":"1"}),"instanceName":"1"}),"instanceName":"1"}),"instanceName":"1"});
            var Q496;
            Q496=makeQuery(id+"F11.opPattern","COPY",BODY,{"derivedFrom":makeQuery(id+"F9.opPattern","COPY",BODY,{"derivedFrom":makeQuery(id+"F6.opPattern","COPY",BODY,{"derivedFrom":makeQuery(id+"F4.opPattern","COPY",BODY,{"derivedFrom":makeQuery(id+"F2.opPattern","COPY",BODY,{"derivedFrom":makeQuery(id+"F1.opRevolve","SWEPT_BODY",BODY,{"disambiguationData":[OSD([sQuery(id+"F0.wireOp",EDGE,"E1")])]}),"instanceName":"1"}),"instanceName":"1"}),"instanceName":"1"}),"instanceName":"1"}),"instanceName":"1"});
            var Q497;
            Q497=makeQuery(id+"F11.opPattern","COPY",BODY,{"derivedFrom":makeQuery(id+"F9.opPattern","COPY",BODY,{"derivedFrom":makeQuery(id+"F6.opPattern","COPY",BODY,{"derivedFrom":makeQuery(id+"F4.opPattern","COPY",BODY,{"derivedFrom":makeQuery(id+"F3.opPattern","COPY",BODY,{"derivedFrom":makeQuery(id+"F2.opPattern","COPY",BODY,{"derivedFrom":makeQuery(id+"F1.opRevolve","SWEPT_BODY",BODY,{"disambiguationData":[OSD([sQuery(id+"F0.wireOp",EDGE,"E1")])]}),"instanceName":"1"}),"instanceName":"1"}),"instanceName":"1"}),"instanceName":"1"}),"instanceName":"1"}),"instanceName":"1"});
            var Q498;
            Q498=makeQuery(id+"F11.opPattern","COPY",BODY,{"derivedFrom":makeQuery(id+"F9.opPattern","COPY",BODY,{"derivedFrom":makeQuery(id+"F6.opPattern","COPY",BODY,{"derivedFrom":makeQuery(id+"F5.opPattern","COPY",BODY,{"derivedFrom":makeQuery(id+"F1.opRevolve","SWEPT_BODY",BODY,{"disambiguationData":[OSD([sQuery(id+"F0.wireOp",EDGE,"E1")])]}),"instanceName":"1"}),"instanceName":"1"}),"instanceName":"1"}),"instanceName":"1"});
            var Q499;
            Q499=makeQuery(id+"F11.opPattern","COPY",BODY,{"derivedFrom":makeQuery(id+"F9.opPattern","COPY",BODY,{"derivedFrom":makeQuery(id+"F6.opPattern","COPY",BODY,{"derivedFrom":makeQuery(id+"F5.opPattern","COPY",BODY,{"derivedFrom":makeQuery(id+"F2.opPattern","COPY",BODY,{"derivedFrom":makeQuery(id+"F1.opRevolve","SWEPT_BODY",BODY,{"disambiguationData":[OSD([sQuery(id+"F0.wireOp",EDGE,"E1")])]}),"instanceName":"1"}),"instanceName":"1"}),"instanceName":"1"}),"instanceName":"1"}),"instanceName":"1"});
            var Q500;
            Q500=makeQuery(id+"F11.opPattern","COPY",BODY,{"derivedFrom":makeQuery(id+"F9.opPattern","COPY",BODY,{"derivedFrom":makeQuery(id+"F6.opPattern","COPY",BODY,{"derivedFrom":makeQuery(id+"F5.opPattern","COPY",BODY,{"derivedFrom":makeQuery(id+"F3.opPattern","COPY",BODY,{"derivedFrom":makeQuery(id+"F2.opPattern","COPY",BODY,{"derivedFrom":makeQuery(id+"F1.opRevolve","SWEPT_BODY",BODY,{"disambiguationData":[OSD([sQuery(id+"F0.wireOp",EDGE,"E1")])]}),"instanceName":"1"}),"instanceName":"1"}),"instanceName":"1"}),"instanceName":"1"}),"instanceName":"1"}),"instanceName":"1"});
            var Q501;
            Q501=makeQuery(id+"F11.opPattern","COPY",BODY,{"derivedFrom":makeQuery(id+"F9.opPattern","COPY",BODY,{"derivedFrom":makeQuery(id+"F6.opPattern","COPY",BODY,{"derivedFrom":makeQuery(id+"F5.opPattern","COPY",BODY,{"derivedFrom":makeQuery(id+"F4.opPattern","COPY",BODY,{"derivedFrom":makeQuery(id+"F1.opRevolve","SWEPT_BODY",BODY,{"disambiguationData":[OSD([sQuery(id+"F0.wireOp",EDGE,"E1")])]}),"instanceName":"1"}),"instanceName":"1"}),"instanceName":"1"}),"instanceName":"1"}),"instanceName":"1"});
            var Q502;
            Q502=makeQuery(id+"F11.opPattern","COPY",BODY,{"derivedFrom":makeQuery(id+"F9.opPattern","COPY",BODY,{"derivedFrom":makeQuery(id+"F6.opPattern","COPY",BODY,{"derivedFrom":makeQuery(id+"F5.opPattern","COPY",BODY,{"derivedFrom":makeQuery(id+"F4.opPattern","COPY",BODY,{"derivedFrom":makeQuery(id+"F2.opPattern","COPY",BODY,{"derivedFrom":makeQuery(id+"F1.opRevolve","SWEPT_BODY",BODY,{"disambiguationData":[OSD([sQuery(id+"F0.wireOp",EDGE,"E1")])]}),"instanceName":"1"}),"instanceName":"1"}),"instanceName":"1"}),"instanceName":"1"}),"instanceName":"1"}),"instanceName":"1"});
            var Q503;
            Q503=makeQuery(id+"F11.opPattern","COPY",BODY,{"derivedFrom":makeQuery(id+"F9.opPattern","COPY",BODY,{"derivedFrom":makeQuery(id+"F6.opPattern","COPY",BODY,{"derivedFrom":makeQuery(id+"F5.opPattern","COPY",BODY,{"derivedFrom":makeQuery(id+"F4.opPattern","COPY",BODY,{"derivedFrom":makeQuery(id+"F3.opPattern","COPY",BODY,{"derivedFrom":makeQuery(id+"F2.opPattern","COPY",BODY,{"derivedFrom":makeQuery(id+"F1.opRevolve","SWEPT_BODY",BODY,{"disambiguationData":[OSD([sQuery(id+"F0.wireOp",EDGE,"E1")])]}),"instanceName":"1"}),"instanceName":"1"}),"instanceName":"1"}),"instanceName":"1"}),"instanceName":"1"}),"instanceName":"1"}),"instanceName":"1"});
            var Q504;
            Q504=makeQuery(id+"F11.opPattern","COPY",BODY,{"derivedFrom":makeQuery(id+"F9.opPattern","COPY",BODY,{"derivedFrom":makeQuery(id+"F7.opPattern","COPY",BODY,{"derivedFrom":makeQuery(id+"F1.opRevolve","SWEPT_BODY",BODY,{"disambiguationData":[OSD([sQuery(id+"F0.wireOp",EDGE,"E1")])]}),"instanceName":"1"}),"instanceName":"1"}),"instanceName":"1"});
            var Q505;
            Q505=makeQuery(id+"F11.opPattern","COPY",BODY,{"derivedFrom":makeQuery(id+"F9.opPattern","COPY",BODY,{"derivedFrom":makeQuery(id+"F7.opPattern","COPY",BODY,{"derivedFrom":makeQuery(id+"F2.opPattern","COPY",BODY,{"derivedFrom":makeQuery(id+"F1.opRevolve","SWEPT_BODY",BODY,{"disambiguationData":[OSD([sQuery(id+"F0.wireOp",EDGE,"E1")])]}),"instanceName":"1"}),"instanceName":"1"}),"instanceName":"1"}),"instanceName":"1"});
            var Q506;
            Q506=makeQuery(id+"F11.opPattern","COPY",BODY,{"derivedFrom":makeQuery(id+"F9.opPattern","COPY",BODY,{"derivedFrom":makeQuery(id+"F7.opPattern","COPY",BODY,{"derivedFrom":makeQuery(id+"F3.opPattern","COPY",BODY,{"derivedFrom":makeQuery(id+"F2.opPattern","COPY",BODY,{"derivedFrom":makeQuery(id+"F1.opRevolve","SWEPT_BODY",BODY,{"disambiguationData":[OSD([sQuery(id+"F0.wireOp",EDGE,"E1")])]}),"instanceName":"1"}),"instanceName":"1"}),"instanceName":"1"}),"instanceName":"1"}),"instanceName":"1"});
            var Q507;
            Q507=makeQuery(id+"F11.opPattern","COPY",BODY,{"derivedFrom":makeQuery(id+"F9.opPattern","COPY",BODY,{"derivedFrom":makeQuery(id+"F7.opPattern","COPY",BODY,{"derivedFrom":makeQuery(id+"F4.opPattern","COPY",BODY,{"derivedFrom":makeQuery(id+"F1.opRevolve","SWEPT_BODY",BODY,{"disambiguationData":[OSD([sQuery(id+"F0.wireOp",EDGE,"E1")])]}),"instanceName":"1"}),"instanceName":"1"}),"instanceName":"1"}),"instanceName":"1"});
            var Q508;
            Q508=makeQuery(id+"F11.opPattern","COPY",BODY,{"derivedFrom":makeQuery(id+"F9.opPattern","COPY",BODY,{"derivedFrom":makeQuery(id+"F7.opPattern","COPY",BODY,{"derivedFrom":makeQuery(id+"F4.opPattern","COPY",BODY,{"derivedFrom":makeQuery(id+"F2.opPattern","COPY",BODY,{"derivedFrom":makeQuery(id+"F1.opRevolve","SWEPT_BODY",BODY,{"disambiguationData":[OSD([sQuery(id+"F0.wireOp",EDGE,"E1")])]}),"instanceName":"1"}),"instanceName":"1"}),"instanceName":"1"}),"instanceName":"1"}),"instanceName":"1"});
            var Q509;
            Q509=makeQuery(id+"F11.opPattern","COPY",BODY,{"derivedFrom":makeQuery(id+"F9.opPattern","COPY",BODY,{"derivedFrom":makeQuery(id+"F7.opPattern","COPY",BODY,{"derivedFrom":makeQuery(id+"F4.opPattern","COPY",BODY,{"derivedFrom":makeQuery(id+"F3.opPattern","COPY",BODY,{"derivedFrom":makeQuery(id+"F2.opPattern","COPY",BODY,{"derivedFrom":makeQuery(id+"F1.opRevolve","SWEPT_BODY",BODY,{"disambiguationData":[OSD([sQuery(id+"F0.wireOp",EDGE,"E1")])]}),"instanceName":"1"}),"instanceName":"1"}),"instanceName":"1"}),"instanceName":"1"}),"instanceName":"1"}),"instanceName":"1"});
            var Q510;
            Q510=makeQuery(id+"F11.opPattern","COPY",BODY,{"derivedFrom":makeQuery(id+"F9.opPattern","COPY",BODY,{"derivedFrom":makeQuery(id+"F7.opPattern","COPY",BODY,{"derivedFrom":makeQuery(id+"F5.opPattern","COPY",BODY,{"derivedFrom":makeQuery(id+"F1.opRevolve","SWEPT_BODY",BODY,{"disambiguationData":[OSD([sQuery(id+"F0.wireOp",EDGE,"E1")])]}),"instanceName":"1"}),"instanceName":"1"}),"instanceName":"1"}),"instanceName":"1"});
            var Q511;
            Q511=makeQuery(id+"F11.opPattern","COPY",BODY,{"derivedFrom":makeQuery(id+"F9.opPattern","COPY",BODY,{"derivedFrom":makeQuery(id+"F7.opPattern","COPY",BODY,{"derivedFrom":makeQuery(id+"F5.opPattern","COPY",BODY,{"derivedFrom":makeQuery(id+"F2.opPattern","COPY",BODY,{"derivedFrom":makeQuery(id+"F1.opRevolve","SWEPT_BODY",BODY,{"disambiguationData":[OSD([sQuery(id+"F0.wireOp",EDGE,"E1")])]}),"instanceName":"1"}),"instanceName":"1"}),"instanceName":"1"}),"instanceName":"1"}),"instanceName":"1"});
            var Q512;
            Q512=makeQuery(id+"F11.opPattern","COPY",BODY,{"derivedFrom":makeQuery(id+"F9.opPattern","COPY",BODY,{"derivedFrom":makeQuery(id+"F7.opPattern","COPY",BODY,{"derivedFrom":makeQuery(id+"F5.opPattern","COPY",BODY,{"derivedFrom":makeQuery(id+"F3.opPattern","COPY",BODY,{"derivedFrom":makeQuery(id+"F2.opPattern","COPY",BODY,{"derivedFrom":makeQuery(id+"F1.opRevolve","SWEPT_BODY",BODY,{"disambiguationData":[OSD([sQuery(id+"F0.wireOp",EDGE,"E1")])]}),"instanceName":"1"}),"instanceName":"1"}),"instanceName":"1"}),"instanceName":"1"}),"instanceName":"1"}),"instanceName":"1"});
            var Q513;
            Q513=makeQuery(id+"F11.opPattern","COPY",BODY,{"derivedFrom":makeQuery(id+"F9.opPattern","COPY",BODY,{"derivedFrom":makeQuery(id+"F7.opPattern","COPY",BODY,{"derivedFrom":makeQuery(id+"F5.opPattern","COPY",BODY,{"derivedFrom":makeQuery(id+"F4.opPattern","COPY",BODY,{"derivedFrom":makeQuery(id+"F1.opRevolve","SWEPT_BODY",BODY,{"disambiguationData":[OSD([sQuery(id+"F0.wireOp",EDGE,"E1")])]}),"instanceName":"1"}),"instanceName":"1"}),"instanceName":"1"}),"instanceName":"1"}),"instanceName":"1"});
            var Q514;
            Q514=makeQuery(id+"F11.opPattern","COPY",BODY,{"derivedFrom":makeQuery(id+"F9.opPattern","COPY",BODY,{"derivedFrom":makeQuery(id+"F7.opPattern","COPY",BODY,{"derivedFrom":makeQuery(id+"F5.opPattern","COPY",BODY,{"derivedFrom":makeQuery(id+"F4.opPattern","COPY",BODY,{"derivedFrom":makeQuery(id+"F2.opPattern","COPY",BODY,{"derivedFrom":makeQuery(id+"F1.opRevolve","SWEPT_BODY",BODY,{"disambiguationData":[OSD([sQuery(id+"F0.wireOp",EDGE,"E1")])]}),"instanceName":"1"}),"instanceName":"1"}),"instanceName":"1"}),"instanceName":"1"}),"instanceName":"1"}),"instanceName":"1"});
            var Q515;
            Q515=makeQuery(id+"F11.opPattern","COPY",BODY,{"derivedFrom":makeQuery(id+"F9.opPattern","COPY",BODY,{"derivedFrom":makeQuery(id+"F7.opPattern","COPY",BODY,{"derivedFrom":makeQuery(id+"F5.opPattern","COPY",BODY,{"derivedFrom":makeQuery(id+"F4.opPattern","COPY",BODY,{"derivedFrom":makeQuery(id+"F3.opPattern","COPY",BODY,{"derivedFrom":makeQuery(id+"F2.opPattern","COPY",BODY,{"derivedFrom":makeQuery(id+"F1.opRevolve","SWEPT_BODY",BODY,{"disambiguationData":[OSD([sQuery(id+"F0.wireOp",EDGE,"E1")])]}),"instanceName":"1"}),"instanceName":"1"}),"instanceName":"1"}),"instanceName":"1"}),"instanceName":"1"}),"instanceName":"1"}),"instanceName":"1"});
            var Q516;
            Q516=makeQuery(id+"F11.opPattern","COPY",BODY,{"derivedFrom":makeQuery(id+"F9.opPattern","COPY",BODY,{"derivedFrom":makeQuery(id+"F7.opPattern","COPY",BODY,{"derivedFrom":makeQuery(id+"F6.opPattern","COPY",BODY,{"derivedFrom":makeQuery(id+"F1.opRevolve","SWEPT_BODY",BODY,{"disambiguationData":[OSD([sQuery(id+"F0.wireOp",EDGE,"E1")])]}),"instanceName":"1"}),"instanceName":"1"}),"instanceName":"1"}),"instanceName":"1"});
            var Q517;
            Q517=makeQuery(id+"F11.opPattern","COPY",BODY,{"derivedFrom":makeQuery(id+"F9.opPattern","COPY",BODY,{"derivedFrom":makeQuery(id+"F7.opPattern","COPY",BODY,{"derivedFrom":makeQuery(id+"F6.opPattern","COPY",BODY,{"derivedFrom":makeQuery(id+"F2.opPattern","COPY",BODY,{"derivedFrom":makeQuery(id+"F1.opRevolve","SWEPT_BODY",BODY,{"disambiguationData":[OSD([sQuery(id+"F0.wireOp",EDGE,"E1")])]}),"instanceName":"1"}),"instanceName":"1"}),"instanceName":"1"}),"instanceName":"1"}),"instanceName":"1"});
            var Q518;
            Q518=makeQuery(id+"F11.opPattern","COPY",BODY,{"derivedFrom":makeQuery(id+"F9.opPattern","COPY",BODY,{"derivedFrom":makeQuery(id+"F7.opPattern","COPY",BODY,{"derivedFrom":makeQuery(id+"F6.opPattern","COPY",BODY,{"derivedFrom":makeQuery(id+"F3.opPattern","COPY",BODY,{"derivedFrom":makeQuery(id+"F2.opPattern","COPY",BODY,{"derivedFrom":makeQuery(id+"F1.opRevolve","SWEPT_BODY",BODY,{"disambiguationData":[OSD([sQuery(id+"F0.wireOp",EDGE,"E1")])]}),"instanceName":"1"}),"instanceName":"1"}),"instanceName":"1"}),"instanceName":"1"}),"instanceName":"1"}),"instanceName":"1"});
            var Q519;
            Q519=makeQuery(id+"F11.opPattern","COPY",BODY,{"derivedFrom":makeQuery(id+"F9.opPattern","COPY",BODY,{"derivedFrom":makeQuery(id+"F7.opPattern","COPY",BODY,{"derivedFrom":makeQuery(id+"F6.opPattern","COPY",BODY,{"derivedFrom":makeQuery(id+"F4.opPattern","COPY",BODY,{"derivedFrom":makeQuery(id+"F1.opRevolve","SWEPT_BODY",BODY,{"disambiguationData":[OSD([sQuery(id+"F0.wireOp",EDGE,"E1")])]}),"instanceName":"1"}),"instanceName":"1"}),"instanceName":"1"}),"instanceName":"1"}),"instanceName":"1"});
            var Q520;
            Q520=makeQuery(id+"F11.opPattern","COPY",BODY,{"derivedFrom":makeQuery(id+"F9.opPattern","COPY",BODY,{"derivedFrom":makeQuery(id+"F7.opPattern","COPY",BODY,{"derivedFrom":makeQuery(id+"F6.opPattern","COPY",BODY,{"derivedFrom":makeQuery(id+"F4.opPattern","COPY",BODY,{"derivedFrom":makeQuery(id+"F2.opPattern","COPY",BODY,{"derivedFrom":makeQuery(id+"F1.opRevolve","SWEPT_BODY",BODY,{"disambiguationData":[OSD([sQuery(id+"F0.wireOp",EDGE,"E1")])]}),"instanceName":"1"}),"instanceName":"1"}),"instanceName":"1"}),"instanceName":"1"}),"instanceName":"1"}),"instanceName":"1"});
            var Q521;
            Q521=makeQuery(id+"F11.opPattern","COPY",BODY,{"derivedFrom":makeQuery(id+"F9.opPattern","COPY",BODY,{"derivedFrom":makeQuery(id+"F7.opPattern","COPY",BODY,{"derivedFrom":makeQuery(id+"F6.opPattern","COPY",BODY,{"derivedFrom":makeQuery(id+"F4.opPattern","COPY",BODY,{"derivedFrom":makeQuery(id+"F3.opPattern","COPY",BODY,{"derivedFrom":makeQuery(id+"F2.opPattern","COPY",BODY,{"derivedFrom":makeQuery(id+"F1.opRevolve","SWEPT_BODY",BODY,{"disambiguationData":[OSD([sQuery(id+"F0.wireOp",EDGE,"E1")])]}),"instanceName":"1"}),"instanceName":"1"}),"instanceName":"1"}),"instanceName":"1"}),"instanceName":"1"}),"instanceName":"1"}),"instanceName":"1"});
            var Q522;
            Q522=makeQuery(id+"F11.opPattern","COPY",BODY,{"derivedFrom":makeQuery(id+"F9.opPattern","COPY",BODY,{"derivedFrom":makeQuery(id+"F7.opPattern","COPY",BODY,{"derivedFrom":makeQuery(id+"F6.opPattern","COPY",BODY,{"derivedFrom":makeQuery(id+"F5.opPattern","COPY",BODY,{"derivedFrom":makeQuery(id+"F1.opRevolve","SWEPT_BODY",BODY,{"disambiguationData":[OSD([sQuery(id+"F0.wireOp",EDGE,"E1")])]}),"instanceName":"1"}),"instanceName":"1"}),"instanceName":"1"}),"instanceName":"1"}),"instanceName":"1"});
            var Q523;
            Q523=makeQuery(id+"F11.opPattern","COPY",BODY,{"derivedFrom":makeQuery(id+"F9.opPattern","COPY",BODY,{"derivedFrom":makeQuery(id+"F7.opPattern","COPY",BODY,{"derivedFrom":makeQuery(id+"F6.opPattern","COPY",BODY,{"derivedFrom":makeQuery(id+"F5.opPattern","COPY",BODY,{"derivedFrom":makeQuery(id+"F2.opPattern","COPY",BODY,{"derivedFrom":makeQuery(id+"F1.opRevolve","SWEPT_BODY",BODY,{"disambiguationData":[OSD([sQuery(id+"F0.wireOp",EDGE,"E1")])]}),"instanceName":"1"}),"instanceName":"1"}),"instanceName":"1"}),"instanceName":"1"}),"instanceName":"1"}),"instanceName":"1"});
            var Q524;
            Q524=makeQuery(id+"F11.opPattern","COPY",BODY,{"derivedFrom":makeQuery(id+"F9.opPattern","COPY",BODY,{"derivedFrom":makeQuery(id+"F7.opPattern","COPY",BODY,{"derivedFrom":makeQuery(id+"F6.opPattern","COPY",BODY,{"derivedFrom":makeQuery(id+"F5.opPattern","COPY",BODY,{"derivedFrom":makeQuery(id+"F3.opPattern","COPY",BODY,{"derivedFrom":makeQuery(id+"F2.opPattern","COPY",BODY,{"derivedFrom":makeQuery(id+"F1.opRevolve","SWEPT_BODY",BODY,{"disambiguationData":[OSD([sQuery(id+"F0.wireOp",EDGE,"E1")])]}),"instanceName":"1"}),"instanceName":"1"}),"instanceName":"1"}),"instanceName":"1"}),"instanceName":"1"}),"instanceName":"1"}),"instanceName":"1"});
            var Q525;
            Q525=makeQuery(id+"F11.opPattern","COPY",BODY,{"derivedFrom":makeQuery(id+"F9.opPattern","COPY",BODY,{"derivedFrom":makeQuery(id+"F7.opPattern","COPY",BODY,{"derivedFrom":makeQuery(id+"F6.opPattern","COPY",BODY,{"derivedFrom":makeQuery(id+"F5.opPattern","COPY",BODY,{"derivedFrom":makeQuery(id+"F4.opPattern","COPY",BODY,{"derivedFrom":makeQuery(id+"F1.opRevolve","SWEPT_BODY",BODY,{"disambiguationData":[OSD([sQuery(id+"F0.wireOp",EDGE,"E1")])]}),"instanceName":"1"}),"instanceName":"1"}),"instanceName":"1"}),"instanceName":"1"}),"instanceName":"1"}),"instanceName":"1"});
            var Q526;
            Q526=makeQuery(id+"F11.opPattern","COPY",BODY,{"derivedFrom":makeQuery(id+"F9.opPattern","COPY",BODY,{"derivedFrom":makeQuery(id+"F7.opPattern","COPY",BODY,{"derivedFrom":makeQuery(id+"F6.opPattern","COPY",BODY,{"derivedFrom":makeQuery(id+"F5.opPattern","COPY",BODY,{"derivedFrom":makeQuery(id+"F4.opPattern","COPY",BODY,{"derivedFrom":makeQuery(id+"F2.opPattern","COPY",BODY,{"derivedFrom":makeQuery(id+"F1.opRevolve","SWEPT_BODY",BODY,{"disambiguationData":[OSD([sQuery(id+"F0.wireOp",EDGE,"E1")])]}),"instanceName":"1"}),"instanceName":"1"}),"instanceName":"1"}),"instanceName":"1"}),"instanceName":"1"}),"instanceName":"1"}),"instanceName":"1"});
            var Q527;
            Q527=makeQuery(id+"F11.opPattern","COPY",BODY,{"derivedFrom":makeQuery(id+"F9.opPattern","COPY",BODY,{"derivedFrom":makeQuery(id+"F7.opPattern","COPY",BODY,{"derivedFrom":makeQuery(id+"F6.opPattern","COPY",BODY,{"derivedFrom":makeQuery(id+"F5.opPattern","COPY",BODY,{"derivedFrom":makeQuery(id+"F4.opPattern","COPY",BODY,{"derivedFrom":makeQuery(id+"F3.opPattern","COPY",BODY,{"derivedFrom":makeQuery(id+"F2.opPattern","COPY",BODY,{"derivedFrom":makeQuery(id+"F1.opRevolve","SWEPT_BODY",BODY,{"disambiguationData":[OSD([sQuery(id+"F0.wireOp",EDGE,"E1")])]}),"instanceName":"1"}),"instanceName":"1"}),"instanceName":"1"}),"instanceName":"1"}),"instanceName":"1"}),"instanceName":"1"}),"instanceName":"1"}),"instanceName":"1"});
            var Q528;
            Q528=makeQuery(id+"F11.opPattern","COPY",BODY,{"derivedFrom":makeQuery(id+"F9.opPattern","COPY",BODY,{"derivedFrom":makeQuery(id+"F8.opPattern","COPY",BODY,{"derivedFrom":makeQuery(id+"F1.opRevolve","SWEPT_BODY",BODY,{"disambiguationData":[OSD([sQuery(id+"F0.wireOp",EDGE,"E1")])]}),"instanceName":"1"}),"instanceName":"1"}),"instanceName":"1"});
            var Q529;
            Q529=makeQuery(id+"F11.opPattern","COPY",BODY,{"derivedFrom":makeQuery(id+"F9.opPattern","COPY",BODY,{"derivedFrom":makeQuery(id+"F8.opPattern","COPY",BODY,{"derivedFrom":makeQuery(id+"F2.opPattern","COPY",BODY,{"derivedFrom":makeQuery(id+"F1.opRevolve","SWEPT_BODY",BODY,{"disambiguationData":[OSD([sQuery(id+"F0.wireOp",EDGE,"E1")])]}),"instanceName":"1"}),"instanceName":"1"}),"instanceName":"1"}),"instanceName":"1"});
            var Q530;
            Q530=makeQuery(id+"F11.opPattern","COPY",BODY,{"derivedFrom":makeQuery(id+"F9.opPattern","COPY",BODY,{"derivedFrom":makeQuery(id+"F8.opPattern","COPY",BODY,{"derivedFrom":makeQuery(id+"F3.opPattern","COPY",BODY,{"derivedFrom":makeQuery(id+"F2.opPattern","COPY",BODY,{"derivedFrom":makeQuery(id+"F1.opRevolve","SWEPT_BODY",BODY,{"disambiguationData":[OSD([sQuery(id+"F0.wireOp",EDGE,"E1")])]}),"instanceName":"1"}),"instanceName":"1"}),"instanceName":"1"}),"instanceName":"1"}),"instanceName":"1"});
            var Q531;
            Q531=makeQuery(id+"F11.opPattern","COPY",BODY,{"derivedFrom":makeQuery(id+"F9.opPattern","COPY",BODY,{"derivedFrom":makeQuery(id+"F8.opPattern","COPY",BODY,{"derivedFrom":makeQuery(id+"F4.opPattern","COPY",BODY,{"derivedFrom":makeQuery(id+"F1.opRevolve","SWEPT_BODY",BODY,{"disambiguationData":[OSD([sQuery(id+"F0.wireOp",EDGE,"E1")])]}),"instanceName":"1"}),"instanceName":"1"}),"instanceName":"1"}),"instanceName":"1"});
            var Q532;
            Q532=makeQuery(id+"F11.opPattern","COPY",BODY,{"derivedFrom":makeQuery(id+"F9.opPattern","COPY",BODY,{"derivedFrom":makeQuery(id+"F8.opPattern","COPY",BODY,{"derivedFrom":makeQuery(id+"F4.opPattern","COPY",BODY,{"derivedFrom":makeQuery(id+"F2.opPattern","COPY",BODY,{"derivedFrom":makeQuery(id+"F1.opRevolve","SWEPT_BODY",BODY,{"disambiguationData":[OSD([sQuery(id+"F0.wireOp",EDGE,"E1")])]}),"instanceName":"1"}),"instanceName":"1"}),"instanceName":"1"}),"instanceName":"1"}),"instanceName":"1"});
            var Q533;
            Q533=makeQuery(id+"F11.opPattern","COPY",BODY,{"derivedFrom":makeQuery(id+"F9.opPattern","COPY",BODY,{"derivedFrom":makeQuery(id+"F8.opPattern","COPY",BODY,{"derivedFrom":makeQuery(id+"F4.opPattern","COPY",BODY,{"derivedFrom":makeQuery(id+"F3.opPattern","COPY",BODY,{"derivedFrom":makeQuery(id+"F2.opPattern","COPY",BODY,{"derivedFrom":makeQuery(id+"F1.opRevolve","SWEPT_BODY",BODY,{"disambiguationData":[OSD([sQuery(id+"F0.wireOp",EDGE,"E1")])]}),"instanceName":"1"}),"instanceName":"1"}),"instanceName":"1"}),"instanceName":"1"}),"instanceName":"1"}),"instanceName":"1"});
            var Q534;
            Q534=makeQuery(id+"F11.opPattern","COPY",BODY,{"derivedFrom":makeQuery(id+"F9.opPattern","COPY",BODY,{"derivedFrom":makeQuery(id+"F8.opPattern","COPY",BODY,{"derivedFrom":makeQuery(id+"F5.opPattern","COPY",BODY,{"derivedFrom":makeQuery(id+"F1.opRevolve","SWEPT_BODY",BODY,{"disambiguationData":[OSD([sQuery(id+"F0.wireOp",EDGE,"E1")])]}),"instanceName":"1"}),"instanceName":"1"}),"instanceName":"1"}),"instanceName":"1"});
            var Q535;
            Q535=makeQuery(id+"F11.opPattern","COPY",BODY,{"derivedFrom":makeQuery(id+"F9.opPattern","COPY",BODY,{"derivedFrom":makeQuery(id+"F8.opPattern","COPY",BODY,{"derivedFrom":makeQuery(id+"F5.opPattern","COPY",BODY,{"derivedFrom":makeQuery(id+"F2.opPattern","COPY",BODY,{"derivedFrom":makeQuery(id+"F1.opRevolve","SWEPT_BODY",BODY,{"disambiguationData":[OSD([sQuery(id+"F0.wireOp",EDGE,"E1")])]}),"instanceName":"1"}),"instanceName":"1"}),"instanceName":"1"}),"instanceName":"1"}),"instanceName":"1"});
            var Q536;
            Q536=makeQuery(id+"F11.opPattern","COPY",BODY,{"derivedFrom":makeQuery(id+"F9.opPattern","COPY",BODY,{"derivedFrom":makeQuery(id+"F8.opPattern","COPY",BODY,{"derivedFrom":makeQuery(id+"F5.opPattern","COPY",BODY,{"derivedFrom":makeQuery(id+"F3.opPattern","COPY",BODY,{"derivedFrom":makeQuery(id+"F2.opPattern","COPY",BODY,{"derivedFrom":makeQuery(id+"F1.opRevolve","SWEPT_BODY",BODY,{"disambiguationData":[OSD([sQuery(id+"F0.wireOp",EDGE,"E1")])]}),"instanceName":"1"}),"instanceName":"1"}),"instanceName":"1"}),"instanceName":"1"}),"instanceName":"1"}),"instanceName":"1"});
            var Q537;
            Q537=makeQuery(id+"F11.opPattern","COPY",BODY,{"derivedFrom":makeQuery(id+"F9.opPattern","COPY",BODY,{"derivedFrom":makeQuery(id+"F8.opPattern","COPY",BODY,{"derivedFrom":makeQuery(id+"F5.opPattern","COPY",BODY,{"derivedFrom":makeQuery(id+"F4.opPattern","COPY",BODY,{"derivedFrom":makeQuery(id+"F1.opRevolve","SWEPT_BODY",BODY,{"disambiguationData":[OSD([sQuery(id+"F0.wireOp",EDGE,"E1")])]}),"instanceName":"1"}),"instanceName":"1"}),"instanceName":"1"}),"instanceName":"1"}),"instanceName":"1"});
            var Q538;
            Q538=makeQuery(id+"F11.opPattern","COPY",BODY,{"derivedFrom":makeQuery(id+"F9.opPattern","COPY",BODY,{"derivedFrom":makeQuery(id+"F8.opPattern","COPY",BODY,{"derivedFrom":makeQuery(id+"F5.opPattern","COPY",BODY,{"derivedFrom":makeQuery(id+"F4.opPattern","COPY",BODY,{"derivedFrom":makeQuery(id+"F2.opPattern","COPY",BODY,{"derivedFrom":makeQuery(id+"F1.opRevolve","SWEPT_BODY",BODY,{"disambiguationData":[OSD([sQuery(id+"F0.wireOp",EDGE,"E1")])]}),"instanceName":"1"}),"instanceName":"1"}),"instanceName":"1"}),"instanceName":"1"}),"instanceName":"1"}),"instanceName":"1"});
            var Q539;
            Q539=makeQuery(id+"F11.opPattern","COPY",BODY,{"derivedFrom":makeQuery(id+"F9.opPattern","COPY",BODY,{"derivedFrom":makeQuery(id+"F8.opPattern","COPY",BODY,{"derivedFrom":makeQuery(id+"F5.opPattern","COPY",BODY,{"derivedFrom":makeQuery(id+"F4.opPattern","COPY",BODY,{"derivedFrom":makeQuery(id+"F3.opPattern","COPY",BODY,{"derivedFrom":makeQuery(id+"F2.opPattern","COPY",BODY,{"derivedFrom":makeQuery(id+"F1.opRevolve","SWEPT_BODY",BODY,{"disambiguationData":[OSD([sQuery(id+"F0.wireOp",EDGE,"E1")])]}),"instanceName":"1"}),"instanceName":"1"}),"instanceName":"1"}),"instanceName":"1"}),"instanceName":"1"}),"instanceName":"1"}),"instanceName":"1"});
            var Q540;
            Q540=makeQuery(id+"F11.opPattern","COPY",BODY,{"derivedFrom":makeQuery(id+"F9.opPattern","COPY",BODY,{"derivedFrom":makeQuery(id+"F8.opPattern","COPY",BODY,{"derivedFrom":makeQuery(id+"F6.opPattern","COPY",BODY,{"derivedFrom":makeQuery(id+"F1.opRevolve","SWEPT_BODY",BODY,{"disambiguationData":[OSD([sQuery(id+"F0.wireOp",EDGE,"E1")])]}),"instanceName":"1"}),"instanceName":"1"}),"instanceName":"1"}),"instanceName":"1"});
            var Q541;
            Q541=makeQuery(id+"F11.opPattern","COPY",BODY,{"derivedFrom":makeQuery(id+"F9.opPattern","COPY",BODY,{"derivedFrom":makeQuery(id+"F8.opPattern","COPY",BODY,{"derivedFrom":makeQuery(id+"F6.opPattern","COPY",BODY,{"derivedFrom":makeQuery(id+"F2.opPattern","COPY",BODY,{"derivedFrom":makeQuery(id+"F1.opRevolve","SWEPT_BODY",BODY,{"disambiguationData":[OSD([sQuery(id+"F0.wireOp",EDGE,"E1")])]}),"instanceName":"1"}),"instanceName":"1"}),"instanceName":"1"}),"instanceName":"1"}),"instanceName":"1"});
            var Q542;
            Q542=makeQuery(id+"F11.opPattern","COPY",BODY,{"derivedFrom":makeQuery(id+"F9.opPattern","COPY",BODY,{"derivedFrom":makeQuery(id+"F8.opPattern","COPY",BODY,{"derivedFrom":makeQuery(id+"F6.opPattern","COPY",BODY,{"derivedFrom":makeQuery(id+"F3.opPattern","COPY",BODY,{"derivedFrom":makeQuery(id+"F2.opPattern","COPY",BODY,{"derivedFrom":makeQuery(id+"F1.opRevolve","SWEPT_BODY",BODY,{"disambiguationData":[OSD([sQuery(id+"F0.wireOp",EDGE,"E1")])]}),"instanceName":"1"}),"instanceName":"1"}),"instanceName":"1"}),"instanceName":"1"}),"instanceName":"1"}),"instanceName":"1"});
            var Q543;
            Q543=makeQuery(id+"F11.opPattern","COPY",BODY,{"derivedFrom":makeQuery(id+"F9.opPattern","COPY",BODY,{"derivedFrom":makeQuery(id+"F8.opPattern","COPY",BODY,{"derivedFrom":makeQuery(id+"F6.opPattern","COPY",BODY,{"derivedFrom":makeQuery(id+"F4.opPattern","COPY",BODY,{"derivedFrom":makeQuery(id+"F1.opRevolve","SWEPT_BODY",BODY,{"disambiguationData":[OSD([sQuery(id+"F0.wireOp",EDGE,"E1")])]}),"instanceName":"1"}),"instanceName":"1"}),"instanceName":"1"}),"instanceName":"1"}),"instanceName":"1"});
            var Q544;
            Q544=makeQuery(id+"F11.opPattern","COPY",BODY,{"derivedFrom":makeQuery(id+"F9.opPattern","COPY",BODY,{"derivedFrom":makeQuery(id+"F8.opPattern","COPY",BODY,{"derivedFrom":makeQuery(id+"F6.opPattern","COPY",BODY,{"derivedFrom":makeQuery(id+"F4.opPattern","COPY",BODY,{"derivedFrom":makeQuery(id+"F2.opPattern","COPY",BODY,{"derivedFrom":makeQuery(id+"F1.opRevolve","SWEPT_BODY",BODY,{"disambiguationData":[OSD([sQuery(id+"F0.wireOp",EDGE,"E1")])]}),"instanceName":"1"}),"instanceName":"1"}),"instanceName":"1"}),"instanceName":"1"}),"instanceName":"1"}),"instanceName":"1"});
            var Q545;
            Q545=makeQuery(id+"F11.opPattern","COPY",BODY,{"derivedFrom":makeQuery(id+"F9.opPattern","COPY",BODY,{"derivedFrom":makeQuery(id+"F8.opPattern","COPY",BODY,{"derivedFrom":makeQuery(id+"F6.opPattern","COPY",BODY,{"derivedFrom":makeQuery(id+"F4.opPattern","COPY",BODY,{"derivedFrom":makeQuery(id+"F3.opPattern","COPY",BODY,{"derivedFrom":makeQuery(id+"F2.opPattern","COPY",BODY,{"derivedFrom":makeQuery(id+"F1.opRevolve","SWEPT_BODY",BODY,{"disambiguationData":[OSD([sQuery(id+"F0.wireOp",EDGE,"E1")])]}),"instanceName":"1"}),"instanceName":"1"}),"instanceName":"1"}),"instanceName":"1"}),"instanceName":"1"}),"instanceName":"1"}),"instanceName":"1"});
            var Q546;
            Q546=makeQuery(id+"F11.opPattern","COPY",BODY,{"derivedFrom":makeQuery(id+"F9.opPattern","COPY",BODY,{"derivedFrom":makeQuery(id+"F8.opPattern","COPY",BODY,{"derivedFrom":makeQuery(id+"F6.opPattern","COPY",BODY,{"derivedFrom":makeQuery(id+"F5.opPattern","COPY",BODY,{"derivedFrom":makeQuery(id+"F1.opRevolve","SWEPT_BODY",BODY,{"disambiguationData":[OSD([sQuery(id+"F0.wireOp",EDGE,"E1")])]}),"instanceName":"1"}),"instanceName":"1"}),"instanceName":"1"}),"instanceName":"1"}),"instanceName":"1"});
            var Q547;
            Q547=makeQuery(id+"F11.opPattern","COPY",BODY,{"derivedFrom":makeQuery(id+"F9.opPattern","COPY",BODY,{"derivedFrom":makeQuery(id+"F8.opPattern","COPY",BODY,{"derivedFrom":makeQuery(id+"F6.opPattern","COPY",BODY,{"derivedFrom":makeQuery(id+"F5.opPattern","COPY",BODY,{"derivedFrom":makeQuery(id+"F2.opPattern","COPY",BODY,{"derivedFrom":makeQuery(id+"F1.opRevolve","SWEPT_BODY",BODY,{"disambiguationData":[OSD([sQuery(id+"F0.wireOp",EDGE,"E1")])]}),"instanceName":"1"}),"instanceName":"1"}),"instanceName":"1"}),"instanceName":"1"}),"instanceName":"1"}),"instanceName":"1"});
            var Q548;
            Q548=makeQuery(id+"F11.opPattern","COPY",BODY,{"derivedFrom":makeQuery(id+"F9.opPattern","COPY",BODY,{"derivedFrom":makeQuery(id+"F8.opPattern","COPY",BODY,{"derivedFrom":makeQuery(id+"F6.opPattern","COPY",BODY,{"derivedFrom":makeQuery(id+"F5.opPattern","COPY",BODY,{"derivedFrom":makeQuery(id+"F3.opPattern","COPY",BODY,{"derivedFrom":makeQuery(id+"F2.opPattern","COPY",BODY,{"derivedFrom":makeQuery(id+"F1.opRevolve","SWEPT_BODY",BODY,{"disambiguationData":[OSD([sQuery(id+"F0.wireOp",EDGE,"E1")])]}),"instanceName":"1"}),"instanceName":"1"}),"instanceName":"1"}),"instanceName":"1"}),"instanceName":"1"}),"instanceName":"1"}),"instanceName":"1"});
            var Q549;
            Q549=makeQuery(id+"F11.opPattern","COPY",BODY,{"derivedFrom":makeQuery(id+"F9.opPattern","COPY",BODY,{"derivedFrom":makeQuery(id+"F8.opPattern","COPY",BODY,{"derivedFrom":makeQuery(id+"F6.opPattern","COPY",BODY,{"derivedFrom":makeQuery(id+"F5.opPattern","COPY",BODY,{"derivedFrom":makeQuery(id+"F4.opPattern","COPY",BODY,{"derivedFrom":makeQuery(id+"F1.opRevolve","SWEPT_BODY",BODY,{"disambiguationData":[OSD([sQuery(id+"F0.wireOp",EDGE,"E1")])]}),"instanceName":"1"}),"instanceName":"1"}),"instanceName":"1"}),"instanceName":"1"}),"instanceName":"1"}),"instanceName":"1"});
            var Q550;
            Q550=makeQuery(id+"F11.opPattern","COPY",BODY,{"derivedFrom":makeQuery(id+"F9.opPattern","COPY",BODY,{"derivedFrom":makeQuery(id+"F8.opPattern","COPY",BODY,{"derivedFrom":makeQuery(id+"F6.opPattern","COPY",BODY,{"derivedFrom":makeQuery(id+"F5.opPattern","COPY",BODY,{"derivedFrom":makeQuery(id+"F4.opPattern","COPY",BODY,{"derivedFrom":makeQuery(id+"F2.opPattern","COPY",BODY,{"derivedFrom":makeQuery(id+"F1.opRevolve","SWEPT_BODY",BODY,{"disambiguationData":[OSD([sQuery(id+"F0.wireOp",EDGE,"E1")])]}),"instanceName":"1"}),"instanceName":"1"}),"instanceName":"1"}),"instanceName":"1"}),"instanceName":"1"}),"instanceName":"1"}),"instanceName":"1"});
            var Q551;
            Q551=makeQuery(id+"F11.opPattern","COPY",BODY,{"derivedFrom":makeQuery(id+"F9.opPattern","COPY",BODY,{"derivedFrom":makeQuery(id+"F8.opPattern","COPY",BODY,{"derivedFrom":makeQuery(id+"F6.opPattern","COPY",BODY,{"derivedFrom":makeQuery(id+"F5.opPattern","COPY",BODY,{"derivedFrom":makeQuery(id+"F4.opPattern","COPY",BODY,{"derivedFrom":makeQuery(id+"F3.opPattern","COPY",BODY,{"derivedFrom":makeQuery(id+"F2.opPattern","COPY",BODY,{"derivedFrom":makeQuery(id+"F1.opRevolve","SWEPT_BODY",BODY,{"disambiguationData":[OSD([sQuery(id+"F0.wireOp",EDGE,"E1")])]}),"instanceName":"1"}),"instanceName":"1"}),"instanceName":"1"}),"instanceName":"1"}),"instanceName":"1"}),"instanceName":"1"}),"instanceName":"1"}),"instanceName":"1"});
            var Q552;
            Q552=makeQuery(id+"F11.opPattern","COPY",BODY,{"derivedFrom":makeQuery(id+"F9.opPattern","COPY",BODY,{"derivedFrom":makeQuery(id+"F8.opPattern","COPY",BODY,{"derivedFrom":makeQuery(id+"F7.opPattern","COPY",BODY,{"derivedFrom":makeQuery(id+"F1.opRevolve","SWEPT_BODY",BODY,{"disambiguationData":[OSD([sQuery(id+"F0.wireOp",EDGE,"E1")])]}),"instanceName":"1"}),"instanceName":"1"}),"instanceName":"1"}),"instanceName":"1"});
            var Q553;
            Q553=makeQuery(id+"F11.opPattern","COPY",BODY,{"derivedFrom":makeQuery(id+"F9.opPattern","COPY",BODY,{"derivedFrom":makeQuery(id+"F8.opPattern","COPY",BODY,{"derivedFrom":makeQuery(id+"F7.opPattern","COPY",BODY,{"derivedFrom":makeQuery(id+"F2.opPattern","COPY",BODY,{"derivedFrom":makeQuery(id+"F1.opRevolve","SWEPT_BODY",BODY,{"disambiguationData":[OSD([sQuery(id+"F0.wireOp",EDGE,"E1")])]}),"instanceName":"1"}),"instanceName":"1"}),"instanceName":"1"}),"instanceName":"1"}),"instanceName":"1"});
            var Q554;
            Q554=makeQuery(id+"F11.opPattern","COPY",BODY,{"derivedFrom":makeQuery(id+"F9.opPattern","COPY",BODY,{"derivedFrom":makeQuery(id+"F8.opPattern","COPY",BODY,{"derivedFrom":makeQuery(id+"F7.opPattern","COPY",BODY,{"derivedFrom":makeQuery(id+"F3.opPattern","COPY",BODY,{"derivedFrom":makeQuery(id+"F2.opPattern","COPY",BODY,{"derivedFrom":makeQuery(id+"F1.opRevolve","SWEPT_BODY",BODY,{"disambiguationData":[OSD([sQuery(id+"F0.wireOp",EDGE,"E1")])]}),"instanceName":"1"}),"instanceName":"1"}),"instanceName":"1"}),"instanceName":"1"}),"instanceName":"1"}),"instanceName":"1"});
            var Q555;
            Q555=makeQuery(id+"F11.opPattern","COPY",BODY,{"derivedFrom":makeQuery(id+"F9.opPattern","COPY",BODY,{"derivedFrom":makeQuery(id+"F8.opPattern","COPY",BODY,{"derivedFrom":makeQuery(id+"F7.opPattern","COPY",BODY,{"derivedFrom":makeQuery(id+"F4.opPattern","COPY",BODY,{"derivedFrom":makeQuery(id+"F1.opRevolve","SWEPT_BODY",BODY,{"disambiguationData":[OSD([sQuery(id+"F0.wireOp",EDGE,"E1")])]}),"instanceName":"1"}),"instanceName":"1"}),"instanceName":"1"}),"instanceName":"1"}),"instanceName":"1"});
            var Q556;
            Q556=makeQuery(id+"F11.opPattern","COPY",BODY,{"derivedFrom":makeQuery(id+"F9.opPattern","COPY",BODY,{"derivedFrom":makeQuery(id+"F8.opPattern","COPY",BODY,{"derivedFrom":makeQuery(id+"F7.opPattern","COPY",BODY,{"derivedFrom":makeQuery(id+"F4.opPattern","COPY",BODY,{"derivedFrom":makeQuery(id+"F2.opPattern","COPY",BODY,{"derivedFrom":makeQuery(id+"F1.opRevolve","SWEPT_BODY",BODY,{"disambiguationData":[OSD([sQuery(id+"F0.wireOp",EDGE,"E1")])]}),"instanceName":"1"}),"instanceName":"1"}),"instanceName":"1"}),"instanceName":"1"}),"instanceName":"1"}),"instanceName":"1"});
            var Q557;
            Q557=makeQuery(id+"F11.opPattern","COPY",BODY,{"derivedFrom":makeQuery(id+"F9.opPattern","COPY",BODY,{"derivedFrom":makeQuery(id+"F8.opPattern","COPY",BODY,{"derivedFrom":makeQuery(id+"F7.opPattern","COPY",BODY,{"derivedFrom":makeQuery(id+"F4.opPattern","COPY",BODY,{"derivedFrom":makeQuery(id+"F3.opPattern","COPY",BODY,{"derivedFrom":makeQuery(id+"F2.opPattern","COPY",BODY,{"derivedFrom":makeQuery(id+"F1.opRevolve","SWEPT_BODY",BODY,{"disambiguationData":[OSD([sQuery(id+"F0.wireOp",EDGE,"E1")])]}),"instanceName":"1"}),"instanceName":"1"}),"instanceName":"1"}),"instanceName":"1"}),"instanceName":"1"}),"instanceName":"1"}),"instanceName":"1"});
            var Q558;
            Q558=makeQuery(id+"F11.opPattern","COPY",BODY,{"derivedFrom":makeQuery(id+"F9.opPattern","COPY",BODY,{"derivedFrom":makeQuery(id+"F8.opPattern","COPY",BODY,{"derivedFrom":makeQuery(id+"F7.opPattern","COPY",BODY,{"derivedFrom":makeQuery(id+"F5.opPattern","COPY",BODY,{"derivedFrom":makeQuery(id+"F1.opRevolve","SWEPT_BODY",BODY,{"disambiguationData":[OSD([sQuery(id+"F0.wireOp",EDGE,"E1")])]}),"instanceName":"1"}),"instanceName":"1"}),"instanceName":"1"}),"instanceName":"1"}),"instanceName":"1"});
            var Q559;
            Q559=makeQuery(id+"F11.opPattern","COPY",BODY,{"derivedFrom":makeQuery(id+"F9.opPattern","COPY",BODY,{"derivedFrom":makeQuery(id+"F8.opPattern","COPY",BODY,{"derivedFrom":makeQuery(id+"F7.opPattern","COPY",BODY,{"derivedFrom":makeQuery(id+"F5.opPattern","COPY",BODY,{"derivedFrom":makeQuery(id+"F2.opPattern","COPY",BODY,{"derivedFrom":makeQuery(id+"F1.opRevolve","SWEPT_BODY",BODY,{"disambiguationData":[OSD([sQuery(id+"F0.wireOp",EDGE,"E1")])]}),"instanceName":"1"}),"instanceName":"1"}),"instanceName":"1"}),"instanceName":"1"}),"instanceName":"1"}),"instanceName":"1"});
            var Q560;
            Q560=makeQuery(id+"F11.opPattern","COPY",BODY,{"derivedFrom":makeQuery(id+"F9.opPattern","COPY",BODY,{"derivedFrom":makeQuery(id+"F8.opPattern","COPY",BODY,{"derivedFrom":makeQuery(id+"F7.opPattern","COPY",BODY,{"derivedFrom":makeQuery(id+"F5.opPattern","COPY",BODY,{"derivedFrom":makeQuery(id+"F3.opPattern","COPY",BODY,{"derivedFrom":makeQuery(id+"F2.opPattern","COPY",BODY,{"derivedFrom":makeQuery(id+"F1.opRevolve","SWEPT_BODY",BODY,{"disambiguationData":[OSD([sQuery(id+"F0.wireOp",EDGE,"E1")])]}),"instanceName":"1"}),"instanceName":"1"}),"instanceName":"1"}),"instanceName":"1"}),"instanceName":"1"}),"instanceName":"1"}),"instanceName":"1"});
            var Q561;
            Q561=makeQuery(id+"F11.opPattern","COPY",BODY,{"derivedFrom":makeQuery(id+"F9.opPattern","COPY",BODY,{"derivedFrom":makeQuery(id+"F8.opPattern","COPY",BODY,{"derivedFrom":makeQuery(id+"F7.opPattern","COPY",BODY,{"derivedFrom":makeQuery(id+"F5.opPattern","COPY",BODY,{"derivedFrom":makeQuery(id+"F4.opPattern","COPY",BODY,{"derivedFrom":makeQuery(id+"F1.opRevolve","SWEPT_BODY",BODY,{"disambiguationData":[OSD([sQuery(id+"F0.wireOp",EDGE,"E1")])]}),"instanceName":"1"}),"instanceName":"1"}),"instanceName":"1"}),"instanceName":"1"}),"instanceName":"1"}),"instanceName":"1"});
            var Q562;
            Q562=makeQuery(id+"F11.opPattern","COPY",BODY,{"derivedFrom":makeQuery(id+"F9.opPattern","COPY",BODY,{"derivedFrom":makeQuery(id+"F8.opPattern","COPY",BODY,{"derivedFrom":makeQuery(id+"F7.opPattern","COPY",BODY,{"derivedFrom":makeQuery(id+"F5.opPattern","COPY",BODY,{"derivedFrom":makeQuery(id+"F4.opPattern","COPY",BODY,{"derivedFrom":makeQuery(id+"F2.opPattern","COPY",BODY,{"derivedFrom":makeQuery(id+"F1.opRevolve","SWEPT_BODY",BODY,{"disambiguationData":[OSD([sQuery(id+"F0.wireOp",EDGE,"E1")])]}),"instanceName":"1"}),"instanceName":"1"}),"instanceName":"1"}),"instanceName":"1"}),"instanceName":"1"}),"instanceName":"1"}),"instanceName":"1"});
            var Q563;
            Q563=makeQuery(id+"F11.opPattern","COPY",BODY,{"derivedFrom":makeQuery(id+"F9.opPattern","COPY",BODY,{"derivedFrom":makeQuery(id+"F8.opPattern","COPY",BODY,{"derivedFrom":makeQuery(id+"F7.opPattern","COPY",BODY,{"derivedFrom":makeQuery(id+"F5.opPattern","COPY",BODY,{"derivedFrom":makeQuery(id+"F4.opPattern","COPY",BODY,{"derivedFrom":makeQuery(id+"F3.opPattern","COPY",BODY,{"derivedFrom":makeQuery(id+"F2.opPattern","COPY",BODY,{"derivedFrom":makeQuery(id+"F1.opRevolve","SWEPT_BODY",BODY,{"disambiguationData":[OSD([sQuery(id+"F0.wireOp",EDGE,"E1")])]}),"instanceName":"1"}),"instanceName":"1"}),"instanceName":"1"}),"instanceName":"1"}),"instanceName":"1"}),"instanceName":"1"}),"instanceName":"1"}),"instanceName":"1"});
            var Q564;
            Q564=makeQuery(id+"F11.opPattern","COPY",BODY,{"derivedFrom":makeQuery(id+"F9.opPattern","COPY",BODY,{"derivedFrom":makeQuery(id+"F8.opPattern","COPY",BODY,{"derivedFrom":makeQuery(id+"F7.opPattern","COPY",BODY,{"derivedFrom":makeQuery(id+"F6.opPattern","COPY",BODY,{"derivedFrom":makeQuery(id+"F1.opRevolve","SWEPT_BODY",BODY,{"disambiguationData":[OSD([sQuery(id+"F0.wireOp",EDGE,"E1")])]}),"instanceName":"1"}),"instanceName":"1"}),"instanceName":"1"}),"instanceName":"1"}),"instanceName":"1"});
            var Q565;
            Q565=makeQuery(id+"F11.opPattern","COPY",BODY,{"derivedFrom":makeQuery(id+"F9.opPattern","COPY",BODY,{"derivedFrom":makeQuery(id+"F8.opPattern","COPY",BODY,{"derivedFrom":makeQuery(id+"F7.opPattern","COPY",BODY,{"derivedFrom":makeQuery(id+"F6.opPattern","COPY",BODY,{"derivedFrom":makeQuery(id+"F2.opPattern","COPY",BODY,{"derivedFrom":makeQuery(id+"F1.opRevolve","SWEPT_BODY",BODY,{"disambiguationData":[OSD([sQuery(id+"F0.wireOp",EDGE,"E1")])]}),"instanceName":"1"}),"instanceName":"1"}),"instanceName":"1"}),"instanceName":"1"}),"instanceName":"1"}),"instanceName":"1"});
            var Q566;
            Q566=makeQuery(id+"F11.opPattern","COPY",BODY,{"derivedFrom":makeQuery(id+"F9.opPattern","COPY",BODY,{"derivedFrom":makeQuery(id+"F8.opPattern","COPY",BODY,{"derivedFrom":makeQuery(id+"F7.opPattern","COPY",BODY,{"derivedFrom":makeQuery(id+"F6.opPattern","COPY",BODY,{"derivedFrom":makeQuery(id+"F3.opPattern","COPY",BODY,{"derivedFrom":makeQuery(id+"F2.opPattern","COPY",BODY,{"derivedFrom":makeQuery(id+"F1.opRevolve","SWEPT_BODY",BODY,{"disambiguationData":[OSD([sQuery(id+"F0.wireOp",EDGE,"E1")])]}),"instanceName":"1"}),"instanceName":"1"}),"instanceName":"1"}),"instanceName":"1"}),"instanceName":"1"}),"instanceName":"1"}),"instanceName":"1"});
            var Q567;
            Q567=makeQuery(id+"F11.opPattern","COPY",BODY,{"derivedFrom":makeQuery(id+"F9.opPattern","COPY",BODY,{"derivedFrom":makeQuery(id+"F8.opPattern","COPY",BODY,{"derivedFrom":makeQuery(id+"F7.opPattern","COPY",BODY,{"derivedFrom":makeQuery(id+"F6.opPattern","COPY",BODY,{"derivedFrom":makeQuery(id+"F4.opPattern","COPY",BODY,{"derivedFrom":makeQuery(id+"F1.opRevolve","SWEPT_BODY",BODY,{"disambiguationData":[OSD([sQuery(id+"F0.wireOp",EDGE,"E1")])]}),"instanceName":"1"}),"instanceName":"1"}),"instanceName":"1"}),"instanceName":"1"}),"instanceName":"1"}),"instanceName":"1"});
            var Q568;
            Q568=makeQuery(id+"F11.opPattern","COPY",BODY,{"derivedFrom":makeQuery(id+"F9.opPattern","COPY",BODY,{"derivedFrom":makeQuery(id+"F8.opPattern","COPY",BODY,{"derivedFrom":makeQuery(id+"F7.opPattern","COPY",BODY,{"derivedFrom":makeQuery(id+"F6.opPattern","COPY",BODY,{"derivedFrom":makeQuery(id+"F4.opPattern","COPY",BODY,{"derivedFrom":makeQuery(id+"F2.opPattern","COPY",BODY,{"derivedFrom":makeQuery(id+"F1.opRevolve","SWEPT_BODY",BODY,{"disambiguationData":[OSD([sQuery(id+"F0.wireOp",EDGE,"E1")])]}),"instanceName":"1"}),"instanceName":"1"}),"instanceName":"1"}),"instanceName":"1"}),"instanceName":"1"}),"instanceName":"1"}),"instanceName":"1"});
            var Q569;
            Q569=makeQuery(id+"F11.opPattern","COPY",BODY,{"derivedFrom":makeQuery(id+"F9.opPattern","COPY",BODY,{"derivedFrom":makeQuery(id+"F8.opPattern","COPY",BODY,{"derivedFrom":makeQuery(id+"F7.opPattern","COPY",BODY,{"derivedFrom":makeQuery(id+"F6.opPattern","COPY",BODY,{"derivedFrom":makeQuery(id+"F4.opPattern","COPY",BODY,{"derivedFrom":makeQuery(id+"F3.opPattern","COPY",BODY,{"derivedFrom":makeQuery(id+"F2.opPattern","COPY",BODY,{"derivedFrom":makeQuery(id+"F1.opRevolve","SWEPT_BODY",BODY,{"disambiguationData":[OSD([sQuery(id+"F0.wireOp",EDGE,"E1")])]}),"instanceName":"1"}),"instanceName":"1"}),"instanceName":"1"}),"instanceName":"1"}),"instanceName":"1"}),"instanceName":"1"}),"instanceName":"1"}),"instanceName":"1"});
            var Q570;
            Q570=makeQuery(id+"F11.opPattern","COPY",BODY,{"derivedFrom":makeQuery(id+"F9.opPattern","COPY",BODY,{"derivedFrom":makeQuery(id+"F8.opPattern","COPY",BODY,{"derivedFrom":makeQuery(id+"F7.opPattern","COPY",BODY,{"derivedFrom":makeQuery(id+"F6.opPattern","COPY",BODY,{"derivedFrom":makeQuery(id+"F5.opPattern","COPY",BODY,{"derivedFrom":makeQuery(id+"F1.opRevolve","SWEPT_BODY",BODY,{"disambiguationData":[OSD([sQuery(id+"F0.wireOp",EDGE,"E1")])]}),"instanceName":"1"}),"instanceName":"1"}),"instanceName":"1"}),"instanceName":"1"}),"instanceName":"1"}),"instanceName":"1"});
            var Q571;
            Q571=makeQuery(id+"F11.opPattern","COPY",BODY,{"derivedFrom":makeQuery(id+"F9.opPattern","COPY",BODY,{"derivedFrom":makeQuery(id+"F8.opPattern","COPY",BODY,{"derivedFrom":makeQuery(id+"F7.opPattern","COPY",BODY,{"derivedFrom":makeQuery(id+"F6.opPattern","COPY",BODY,{"derivedFrom":makeQuery(id+"F5.opPattern","COPY",BODY,{"derivedFrom":makeQuery(id+"F2.opPattern","COPY",BODY,{"derivedFrom":makeQuery(id+"F1.opRevolve","SWEPT_BODY",BODY,{"disambiguationData":[OSD([sQuery(id+"F0.wireOp",EDGE,"E1")])]}),"instanceName":"1"}),"instanceName":"1"}),"instanceName":"1"}),"instanceName":"1"}),"instanceName":"1"}),"instanceName":"1"}),"instanceName":"1"});
            var Q572;
            Q572=makeQuery(id+"F11.opPattern","COPY",BODY,{"derivedFrom":makeQuery(id+"F9.opPattern","COPY",BODY,{"derivedFrom":makeQuery(id+"F8.opPattern","COPY",BODY,{"derivedFrom":makeQuery(id+"F7.opPattern","COPY",BODY,{"derivedFrom":makeQuery(id+"F6.opPattern","COPY",BODY,{"derivedFrom":makeQuery(id+"F5.opPattern","COPY",BODY,{"derivedFrom":makeQuery(id+"F3.opPattern","COPY",BODY,{"derivedFrom":makeQuery(id+"F2.opPattern","COPY",BODY,{"derivedFrom":makeQuery(id+"F1.opRevolve","SWEPT_BODY",BODY,{"disambiguationData":[OSD([sQuery(id+"F0.wireOp",EDGE,"E1")])]}),"instanceName":"1"}),"instanceName":"1"}),"instanceName":"1"}),"instanceName":"1"}),"instanceName":"1"}),"instanceName":"1"}),"instanceName":"1"}),"instanceName":"1"});
            var Q573;
            Q573=makeQuery(id+"F11.opPattern","COPY",BODY,{"derivedFrom":makeQuery(id+"F9.opPattern","COPY",BODY,{"derivedFrom":makeQuery(id+"F8.opPattern","COPY",BODY,{"derivedFrom":makeQuery(id+"F7.opPattern","COPY",BODY,{"derivedFrom":makeQuery(id+"F6.opPattern","COPY",BODY,{"derivedFrom":makeQuery(id+"F5.opPattern","COPY",BODY,{"derivedFrom":makeQuery(id+"F4.opPattern","COPY",BODY,{"derivedFrom":makeQuery(id+"F1.opRevolve","SWEPT_BODY",BODY,{"disambiguationData":[OSD([sQuery(id+"F0.wireOp",EDGE,"E1")])]}),"instanceName":"1"}),"instanceName":"1"}),"instanceName":"1"}),"instanceName":"1"}),"instanceName":"1"}),"instanceName":"1"}),"instanceName":"1"});
            var Q574;
            Q574=makeQuery(id+"F11.opPattern","COPY",BODY,{"derivedFrom":makeQuery(id+"F9.opPattern","COPY",BODY,{"derivedFrom":makeQuery(id+"F8.opPattern","COPY",BODY,{"derivedFrom":makeQuery(id+"F7.opPattern","COPY",BODY,{"derivedFrom":makeQuery(id+"F6.opPattern","COPY",BODY,{"derivedFrom":makeQuery(id+"F5.opPattern","COPY",BODY,{"derivedFrom":makeQuery(id+"F4.opPattern","COPY",BODY,{"derivedFrom":makeQuery(id+"F2.opPattern","COPY",BODY,{"derivedFrom":makeQuery(id+"F1.opRevolve","SWEPT_BODY",BODY,{"disambiguationData":[OSD([sQuery(id+"F0.wireOp",EDGE,"E1")])]}),"instanceName":"1"}),"instanceName":"1"}),"instanceName":"1"}),"instanceName":"1"}),"instanceName":"1"}),"instanceName":"1"}),"instanceName":"1"}),"instanceName":"1"});
            var Q575;
            Q575=makeQuery(id+"F11.opPattern","COPY",BODY,{"derivedFrom":makeQuery(id+"F9.opPattern","COPY",BODY,{"derivedFrom":makeQuery(id+"F8.opPattern","COPY",BODY,{"derivedFrom":makeQuery(id+"F7.opPattern","COPY",BODY,{"derivedFrom":makeQuery(id+"F6.opPattern","COPY",BODY,{"derivedFrom":makeQuery(id+"F5.opPattern","COPY",BODY,{"derivedFrom":makeQuery(id+"F4.opPattern","COPY",BODY,{"derivedFrom":makeQuery(id+"F3.opPattern","COPY",BODY,{"derivedFrom":makeQuery(id+"F2.opPattern","COPY",BODY,{"derivedFrom":makeQuery(id+"F1.opRevolve","SWEPT_BODY",BODY,{"disambiguationData":[OSD([sQuery(id+"F0.wireOp",EDGE,"E1")])]}),"instanceName":"1"}),"instanceName":"1"}),"instanceName":"1"}),"instanceName":"1"}),"instanceName":"1"}),"instanceName":"1"}),"instanceName":"1"}),"instanceName":"1"}),"instanceName":"1"});
            var Q576;
            Q576=makeQuery(id+"F11.opPattern","COPY",BODY,{"derivedFrom":makeQuery(id+"F10.opPattern","COPY",BODY,{"derivedFrom":makeQuery(id+"F1.opRevolve","SWEPT_BODY",BODY,{"disambiguationData":[OSD([sQuery(id+"F0.wireOp",EDGE,"E1")])]}),"instanceName":"1"}),"instanceName":"1"});
            var Q577;
            Q577=makeQuery(id+"F11.opPattern","COPY",BODY,{"derivedFrom":makeQuery(id+"F10.opPattern","COPY",BODY,{"derivedFrom":makeQuery(id+"F2.opPattern","COPY",BODY,{"derivedFrom":makeQuery(id+"F1.opRevolve","SWEPT_BODY",BODY,{"disambiguationData":[OSD([sQuery(id+"F0.wireOp",EDGE,"E1")])]}),"instanceName":"1"}),"instanceName":"1"}),"instanceName":"1"});
            var Q578;
            Q578=makeQuery(id+"F11.opPattern","COPY",BODY,{"derivedFrom":makeQuery(id+"F10.opPattern","COPY",BODY,{"derivedFrom":makeQuery(id+"F3.opPattern","COPY",BODY,{"derivedFrom":makeQuery(id+"F2.opPattern","COPY",BODY,{"derivedFrom":makeQuery(id+"F1.opRevolve","SWEPT_BODY",BODY,{"disambiguationData":[OSD([sQuery(id+"F0.wireOp",EDGE,"E1")])]}),"instanceName":"1"}),"instanceName":"1"}),"instanceName":"1"}),"instanceName":"1"});
            var Q579;
            Q579=makeQuery(id+"F11.opPattern","COPY",BODY,{"derivedFrom":makeQuery(id+"F10.opPattern","COPY",BODY,{"derivedFrom":makeQuery(id+"F4.opPattern","COPY",BODY,{"derivedFrom":makeQuery(id+"F1.opRevolve","SWEPT_BODY",BODY,{"disambiguationData":[OSD([sQuery(id+"F0.wireOp",EDGE,"E1")])]}),"instanceName":"1"}),"instanceName":"1"}),"instanceName":"1"});
            var Q580;
            Q580=makeQuery(id+"F11.opPattern","COPY",BODY,{"derivedFrom":makeQuery(id+"F10.opPattern","COPY",BODY,{"derivedFrom":makeQuery(id+"F4.opPattern","COPY",BODY,{"derivedFrom":makeQuery(id+"F2.opPattern","COPY",BODY,{"derivedFrom":makeQuery(id+"F1.opRevolve","SWEPT_BODY",BODY,{"disambiguationData":[OSD([sQuery(id+"F0.wireOp",EDGE,"E1")])]}),"instanceName":"1"}),"instanceName":"1"}),"instanceName":"1"}),"instanceName":"1"});
            var Q581;
            Q581=makeQuery(id+"F11.opPattern","COPY",BODY,{"derivedFrom":makeQuery(id+"F10.opPattern","COPY",BODY,{"derivedFrom":makeQuery(id+"F4.opPattern","COPY",BODY,{"derivedFrom":makeQuery(id+"F3.opPattern","COPY",BODY,{"derivedFrom":makeQuery(id+"F2.opPattern","COPY",BODY,{"derivedFrom":makeQuery(id+"F1.opRevolve","SWEPT_BODY",BODY,{"disambiguationData":[OSD([sQuery(id+"F0.wireOp",EDGE,"E1")])]}),"instanceName":"1"}),"instanceName":"1"}),"instanceName":"1"}),"instanceName":"1"}),"instanceName":"1"});
            var Q582;
            Q582=makeQuery(id+"F11.opPattern","COPY",BODY,{"derivedFrom":makeQuery(id+"F10.opPattern","COPY",BODY,{"derivedFrom":makeQuery(id+"F5.opPattern","COPY",BODY,{"derivedFrom":makeQuery(id+"F1.opRevolve","SWEPT_BODY",BODY,{"disambiguationData":[OSD([sQuery(id+"F0.wireOp",EDGE,"E1")])]}),"instanceName":"1"}),"instanceName":"1"}),"instanceName":"1"});
            var Q583;
            Q583=makeQuery(id+"F11.opPattern","COPY",BODY,{"derivedFrom":makeQuery(id+"F10.opPattern","COPY",BODY,{"derivedFrom":makeQuery(id+"F5.opPattern","COPY",BODY,{"derivedFrom":makeQuery(id+"F2.opPattern","COPY",BODY,{"derivedFrom":makeQuery(id+"F1.opRevolve","SWEPT_BODY",BODY,{"disambiguationData":[OSD([sQuery(id+"F0.wireOp",EDGE,"E1")])]}),"instanceName":"1"}),"instanceName":"1"}),"instanceName":"1"}),"instanceName":"1"});
            var Q584;
            Q584=makeQuery(id+"F11.opPattern","COPY",BODY,{"derivedFrom":makeQuery(id+"F10.opPattern","COPY",BODY,{"derivedFrom":makeQuery(id+"F5.opPattern","COPY",BODY,{"derivedFrom":makeQuery(id+"F3.opPattern","COPY",BODY,{"derivedFrom":makeQuery(id+"F2.opPattern","COPY",BODY,{"derivedFrom":makeQuery(id+"F1.opRevolve","SWEPT_BODY",BODY,{"disambiguationData":[OSD([sQuery(id+"F0.wireOp",EDGE,"E1")])]}),"instanceName":"1"}),"instanceName":"1"}),"instanceName":"1"}),"instanceName":"1"}),"instanceName":"1"});
            var Q585;
            Q585=makeQuery(id+"F11.opPattern","COPY",BODY,{"derivedFrom":makeQuery(id+"F10.opPattern","COPY",BODY,{"derivedFrom":makeQuery(id+"F5.opPattern","COPY",BODY,{"derivedFrom":makeQuery(id+"F4.opPattern","COPY",BODY,{"derivedFrom":makeQuery(id+"F1.opRevolve","SWEPT_BODY",BODY,{"disambiguationData":[OSD([sQuery(id+"F0.wireOp",EDGE,"E1")])]}),"instanceName":"1"}),"instanceName":"1"}),"instanceName":"1"}),"instanceName":"1"});
            var Q586;
            Q586=makeQuery(id+"F11.opPattern","COPY",BODY,{"derivedFrom":makeQuery(id+"F10.opPattern","COPY",BODY,{"derivedFrom":makeQuery(id+"F5.opPattern","COPY",BODY,{"derivedFrom":makeQuery(id+"F4.opPattern","COPY",BODY,{"derivedFrom":makeQuery(id+"F2.opPattern","COPY",BODY,{"derivedFrom":makeQuery(id+"F1.opRevolve","SWEPT_BODY",BODY,{"disambiguationData":[OSD([sQuery(id+"F0.wireOp",EDGE,"E1")])]}),"instanceName":"1"}),"instanceName":"1"}),"instanceName":"1"}),"instanceName":"1"}),"instanceName":"1"});
            var Q587;
            Q587=makeQuery(id+"F11.opPattern","COPY",BODY,{"derivedFrom":makeQuery(id+"F10.opPattern","COPY",BODY,{"derivedFrom":makeQuery(id+"F5.opPattern","COPY",BODY,{"derivedFrom":makeQuery(id+"F4.opPattern","COPY",BODY,{"derivedFrom":makeQuery(id+"F3.opPattern","COPY",BODY,{"derivedFrom":makeQuery(id+"F2.opPattern","COPY",BODY,{"derivedFrom":makeQuery(id+"F1.opRevolve","SWEPT_BODY",BODY,{"disambiguationData":[OSD([sQuery(id+"F0.wireOp",EDGE,"E1")])]}),"instanceName":"1"}),"instanceName":"1"}),"instanceName":"1"}),"instanceName":"1"}),"instanceName":"1"}),"instanceName":"1"});
            var Q588;
            Q588=makeQuery(id+"F11.opPattern","COPY",BODY,{"derivedFrom":makeQuery(id+"F10.opPattern","COPY",BODY,{"derivedFrom":makeQuery(id+"F6.opPattern","COPY",BODY,{"derivedFrom":makeQuery(id+"F1.opRevolve","SWEPT_BODY",BODY,{"disambiguationData":[OSD([sQuery(id+"F0.wireOp",EDGE,"E1")])]}),"instanceName":"1"}),"instanceName":"1"}),"instanceName":"1"});
            var Q589;
            Q589=makeQuery(id+"F11.opPattern","COPY",BODY,{"derivedFrom":makeQuery(id+"F10.opPattern","COPY",BODY,{"derivedFrom":makeQuery(id+"F6.opPattern","COPY",BODY,{"derivedFrom":makeQuery(id+"F2.opPattern","COPY",BODY,{"derivedFrom":makeQuery(id+"F1.opRevolve","SWEPT_BODY",BODY,{"disambiguationData":[OSD([sQuery(id+"F0.wireOp",EDGE,"E1")])]}),"instanceName":"1"}),"instanceName":"1"}),"instanceName":"1"}),"instanceName":"1"});
            var Q590;
            Q590=makeQuery(id+"F11.opPattern","COPY",BODY,{"derivedFrom":makeQuery(id+"F10.opPattern","COPY",BODY,{"derivedFrom":makeQuery(id+"F6.opPattern","COPY",BODY,{"derivedFrom":makeQuery(id+"F3.opPattern","COPY",BODY,{"derivedFrom":makeQuery(id+"F2.opPattern","COPY",BODY,{"derivedFrom":makeQuery(id+"F1.opRevolve","SWEPT_BODY",BODY,{"disambiguationData":[OSD([sQuery(id+"F0.wireOp",EDGE,"E1")])]}),"instanceName":"1"}),"instanceName":"1"}),"instanceName":"1"}),"instanceName":"1"}),"instanceName":"1"});
            var Q591;
            Q591=makeQuery(id+"F11.opPattern","COPY",BODY,{"derivedFrom":makeQuery(id+"F10.opPattern","COPY",BODY,{"derivedFrom":makeQuery(id+"F6.opPattern","COPY",BODY,{"derivedFrom":makeQuery(id+"F4.opPattern","COPY",BODY,{"derivedFrom":makeQuery(id+"F1.opRevolve","SWEPT_BODY",BODY,{"disambiguationData":[OSD([sQuery(id+"F0.wireOp",EDGE,"E1")])]}),"instanceName":"1"}),"instanceName":"1"}),"instanceName":"1"}),"instanceName":"1"});
            var Q592;
            Q592=makeQuery(id+"F11.opPattern","COPY",BODY,{"derivedFrom":makeQuery(id+"F10.opPattern","COPY",BODY,{"derivedFrom":makeQuery(id+"F6.opPattern","COPY",BODY,{"derivedFrom":makeQuery(id+"F4.opPattern","COPY",BODY,{"derivedFrom":makeQuery(id+"F2.opPattern","COPY",BODY,{"derivedFrom":makeQuery(id+"F1.opRevolve","SWEPT_BODY",BODY,{"disambiguationData":[OSD([sQuery(id+"F0.wireOp",EDGE,"E1")])]}),"instanceName":"1"}),"instanceName":"1"}),"instanceName":"1"}),"instanceName":"1"}),"instanceName":"1"});
            var Q593;
            Q593=makeQuery(id+"F11.opPattern","COPY",BODY,{"derivedFrom":makeQuery(id+"F10.opPattern","COPY",BODY,{"derivedFrom":makeQuery(id+"F6.opPattern","COPY",BODY,{"derivedFrom":makeQuery(id+"F4.opPattern","COPY",BODY,{"derivedFrom":makeQuery(id+"F3.opPattern","COPY",BODY,{"derivedFrom":makeQuery(id+"F2.opPattern","COPY",BODY,{"derivedFrom":makeQuery(id+"F1.opRevolve","SWEPT_BODY",BODY,{"disambiguationData":[OSD([sQuery(id+"F0.wireOp",EDGE,"E1")])]}),"instanceName":"1"}),"instanceName":"1"}),"instanceName":"1"}),"instanceName":"1"}),"instanceName":"1"}),"instanceName":"1"});
            var Q594;
            Q594=makeQuery(id+"F11.opPattern","COPY",BODY,{"derivedFrom":makeQuery(id+"F10.opPattern","COPY",BODY,{"derivedFrom":makeQuery(id+"F6.opPattern","COPY",BODY,{"derivedFrom":makeQuery(id+"F5.opPattern","COPY",BODY,{"derivedFrom":makeQuery(id+"F1.opRevolve","SWEPT_BODY",BODY,{"disambiguationData":[OSD([sQuery(id+"F0.wireOp",EDGE,"E1")])]}),"instanceName":"1"}),"instanceName":"1"}),"instanceName":"1"}),"instanceName":"1"});
            var Q595;
            Q595=makeQuery(id+"F11.opPattern","COPY",BODY,{"derivedFrom":makeQuery(id+"F10.opPattern","COPY",BODY,{"derivedFrom":makeQuery(id+"F6.opPattern","COPY",BODY,{"derivedFrom":makeQuery(id+"F5.opPattern","COPY",BODY,{"derivedFrom":makeQuery(id+"F2.opPattern","COPY",BODY,{"derivedFrom":makeQuery(id+"F1.opRevolve","SWEPT_BODY",BODY,{"disambiguationData":[OSD([sQuery(id+"F0.wireOp",EDGE,"E1")])]}),"instanceName":"1"}),"instanceName":"1"}),"instanceName":"1"}),"instanceName":"1"}),"instanceName":"1"});
            var Q596;
            Q596=makeQuery(id+"F11.opPattern","COPY",BODY,{"derivedFrom":makeQuery(id+"F10.opPattern","COPY",BODY,{"derivedFrom":makeQuery(id+"F6.opPattern","COPY",BODY,{"derivedFrom":makeQuery(id+"F5.opPattern","COPY",BODY,{"derivedFrom":makeQuery(id+"F3.opPattern","COPY",BODY,{"derivedFrom":makeQuery(id+"F2.opPattern","COPY",BODY,{"derivedFrom":makeQuery(id+"F1.opRevolve","SWEPT_BODY",BODY,{"disambiguationData":[OSD([sQuery(id+"F0.wireOp",EDGE,"E1")])]}),"instanceName":"1"}),"instanceName":"1"}),"instanceName":"1"}),"instanceName":"1"}),"instanceName":"1"}),"instanceName":"1"});
            var Q597;
            Q597=makeQuery(id+"F11.opPattern","COPY",BODY,{"derivedFrom":makeQuery(id+"F10.opPattern","COPY",BODY,{"derivedFrom":makeQuery(id+"F6.opPattern","COPY",BODY,{"derivedFrom":makeQuery(id+"F5.opPattern","COPY",BODY,{"derivedFrom":makeQuery(id+"F4.opPattern","COPY",BODY,{"derivedFrom":makeQuery(id+"F1.opRevolve","SWEPT_BODY",BODY,{"disambiguationData":[OSD([sQuery(id+"F0.wireOp",EDGE,"E1")])]}),"instanceName":"1"}),"instanceName":"1"}),"instanceName":"1"}),"instanceName":"1"}),"instanceName":"1"});
            var Q598;
            Q598=makeQuery(id+"F11.opPattern","COPY",BODY,{"derivedFrom":makeQuery(id+"F10.opPattern","COPY",BODY,{"derivedFrom":makeQuery(id+"F6.opPattern","COPY",BODY,{"derivedFrom":makeQuery(id+"F5.opPattern","COPY",BODY,{"derivedFrom":makeQuery(id+"F4.opPattern","COPY",BODY,{"derivedFrom":makeQuery(id+"F2.opPattern","COPY",BODY,{"derivedFrom":makeQuery(id+"F1.opRevolve","SWEPT_BODY",BODY,{"disambiguationData":[OSD([sQuery(id+"F0.wireOp",EDGE,"E1")])]}),"instanceName":"1"}),"instanceName":"1"}),"instanceName":"1"}),"instanceName":"1"}),"instanceName":"1"}),"instanceName":"1"});
            var Q599;
            Q599=makeQuery(id+"F11.opPattern","COPY",BODY,{"derivedFrom":makeQuery(id+"F10.opPattern","COPY",BODY,{"derivedFrom":makeQuery(id+"F6.opPattern","COPY",BODY,{"derivedFrom":makeQuery(id+"F5.opPattern","COPY",BODY,{"derivedFrom":makeQuery(id+"F4.opPattern","COPY",BODY,{"derivedFrom":makeQuery(id+"F3.opPattern","COPY",BODY,{"derivedFrom":makeQuery(id+"F2.opPattern","COPY",BODY,{"derivedFrom":makeQuery(id+"F1.opRevolve","SWEPT_BODY",BODY,{"disambiguationData":[OSD([sQuery(id+"F0.wireOp",EDGE,"E1")])]}),"instanceName":"1"}),"instanceName":"1"}),"instanceName":"1"}),"instanceName":"1"}),"instanceName":"1"}),"instanceName":"1"}),"instanceName":"1"});
            var Q600;
            Q600=makeQuery(id+"F11.opPattern","COPY",BODY,{"derivedFrom":makeQuery(id+"F10.opPattern","COPY",BODY,{"derivedFrom":makeQuery(id+"F7.opPattern","COPY",BODY,{"derivedFrom":makeQuery(id+"F1.opRevolve","SWEPT_BODY",BODY,{"disambiguationData":[OSD([sQuery(id+"F0.wireOp",EDGE,"E1")])]}),"instanceName":"1"}),"instanceName":"1"}),"instanceName":"1"});
            var Q601;
            Q601=makeQuery(id+"F11.opPattern","COPY",BODY,{"derivedFrom":makeQuery(id+"F10.opPattern","COPY",BODY,{"derivedFrom":makeQuery(id+"F7.opPattern","COPY",BODY,{"derivedFrom":makeQuery(id+"F2.opPattern","COPY",BODY,{"derivedFrom":makeQuery(id+"F1.opRevolve","SWEPT_BODY",BODY,{"disambiguationData":[OSD([sQuery(id+"F0.wireOp",EDGE,"E1")])]}),"instanceName":"1"}),"instanceName":"1"}),"instanceName":"1"}),"instanceName":"1"});
            var Q602;
            Q602=makeQuery(id+"F11.opPattern","COPY",BODY,{"derivedFrom":makeQuery(id+"F10.opPattern","COPY",BODY,{"derivedFrom":makeQuery(id+"F7.opPattern","COPY",BODY,{"derivedFrom":makeQuery(id+"F3.opPattern","COPY",BODY,{"derivedFrom":makeQuery(id+"F2.opPattern","COPY",BODY,{"derivedFrom":makeQuery(id+"F1.opRevolve","SWEPT_BODY",BODY,{"disambiguationData":[OSD([sQuery(id+"F0.wireOp",EDGE,"E1")])]}),"instanceName":"1"}),"instanceName":"1"}),"instanceName":"1"}),"instanceName":"1"}),"instanceName":"1"});
            var Q603;
            Q603=makeQuery(id+"F11.opPattern","COPY",BODY,{"derivedFrom":makeQuery(id+"F10.opPattern","COPY",BODY,{"derivedFrom":makeQuery(id+"F7.opPattern","COPY",BODY,{"derivedFrom":makeQuery(id+"F4.opPattern","COPY",BODY,{"derivedFrom":makeQuery(id+"F1.opRevolve","SWEPT_BODY",BODY,{"disambiguationData":[OSD([sQuery(id+"F0.wireOp",EDGE,"E1")])]}),"instanceName":"1"}),"instanceName":"1"}),"instanceName":"1"}),"instanceName":"1"});
            var Q604;
            Q604=makeQuery(id+"F11.opPattern","COPY",BODY,{"derivedFrom":makeQuery(id+"F10.opPattern","COPY",BODY,{"derivedFrom":makeQuery(id+"F7.opPattern","COPY",BODY,{"derivedFrom":makeQuery(id+"F4.opPattern","COPY",BODY,{"derivedFrom":makeQuery(id+"F2.opPattern","COPY",BODY,{"derivedFrom":makeQuery(id+"F1.opRevolve","SWEPT_BODY",BODY,{"disambiguationData":[OSD([sQuery(id+"F0.wireOp",EDGE,"E1")])]}),"instanceName":"1"}),"instanceName":"1"}),"instanceName":"1"}),"instanceName":"1"}),"instanceName":"1"});
            var Q605;
            Q605=makeQuery(id+"F11.opPattern","COPY",BODY,{"derivedFrom":makeQuery(id+"F10.opPattern","COPY",BODY,{"derivedFrom":makeQuery(id+"F7.opPattern","COPY",BODY,{"derivedFrom":makeQuery(id+"F4.opPattern","COPY",BODY,{"derivedFrom":makeQuery(id+"F3.opPattern","COPY",BODY,{"derivedFrom":makeQuery(id+"F2.opPattern","COPY",BODY,{"derivedFrom":makeQuery(id+"F1.opRevolve","SWEPT_BODY",BODY,{"disambiguationData":[OSD([sQuery(id+"F0.wireOp",EDGE,"E1")])]}),"instanceName":"1"}),"instanceName":"1"}),"instanceName":"1"}),"instanceName":"1"}),"instanceName":"1"}),"instanceName":"1"});
            var Q606;
            Q606=makeQuery(id+"F11.opPattern","COPY",BODY,{"derivedFrom":makeQuery(id+"F10.opPattern","COPY",BODY,{"derivedFrom":makeQuery(id+"F7.opPattern","COPY",BODY,{"derivedFrom":makeQuery(id+"F5.opPattern","COPY",BODY,{"derivedFrom":makeQuery(id+"F1.opRevolve","SWEPT_BODY",BODY,{"disambiguationData":[OSD([sQuery(id+"F0.wireOp",EDGE,"E1")])]}),"instanceName":"1"}),"instanceName":"1"}),"instanceName":"1"}),"instanceName":"1"});
            var Q607;
            Q607=makeQuery(id+"F11.opPattern","COPY",BODY,{"derivedFrom":makeQuery(id+"F10.opPattern","COPY",BODY,{"derivedFrom":makeQuery(id+"F7.opPattern","COPY",BODY,{"derivedFrom":makeQuery(id+"F5.opPattern","COPY",BODY,{"derivedFrom":makeQuery(id+"F2.opPattern","COPY",BODY,{"derivedFrom":makeQuery(id+"F1.opRevolve","SWEPT_BODY",BODY,{"disambiguationData":[OSD([sQuery(id+"F0.wireOp",EDGE,"E1")])]}),"instanceName":"1"}),"instanceName":"1"}),"instanceName":"1"}),"instanceName":"1"}),"instanceName":"1"});
            var Q608;
            Q608=makeQuery(id+"F11.opPattern","COPY",BODY,{"derivedFrom":makeQuery(id+"F10.opPattern","COPY",BODY,{"derivedFrom":makeQuery(id+"F7.opPattern","COPY",BODY,{"derivedFrom":makeQuery(id+"F5.opPattern","COPY",BODY,{"derivedFrom":makeQuery(id+"F3.opPattern","COPY",BODY,{"derivedFrom":makeQuery(id+"F2.opPattern","COPY",BODY,{"derivedFrom":makeQuery(id+"F1.opRevolve","SWEPT_BODY",BODY,{"disambiguationData":[OSD([sQuery(id+"F0.wireOp",EDGE,"E1")])]}),"instanceName":"1"}),"instanceName":"1"}),"instanceName":"1"}),"instanceName":"1"}),"instanceName":"1"}),"instanceName":"1"});
            var Q609;
            Q609=makeQuery(id+"F11.opPattern","COPY",BODY,{"derivedFrom":makeQuery(id+"F10.opPattern","COPY",BODY,{"derivedFrom":makeQuery(id+"F7.opPattern","COPY",BODY,{"derivedFrom":makeQuery(id+"F5.opPattern","COPY",BODY,{"derivedFrom":makeQuery(id+"F4.opPattern","COPY",BODY,{"derivedFrom":makeQuery(id+"F1.opRevolve","SWEPT_BODY",BODY,{"disambiguationData":[OSD([sQuery(id+"F0.wireOp",EDGE,"E1")])]}),"instanceName":"1"}),"instanceName":"1"}),"instanceName":"1"}),"instanceName":"1"}),"instanceName":"1"});
            var Q610;
            Q610=makeQuery(id+"F11.opPattern","COPY",BODY,{"derivedFrom":makeQuery(id+"F10.opPattern","COPY",BODY,{"derivedFrom":makeQuery(id+"F7.opPattern","COPY",BODY,{"derivedFrom":makeQuery(id+"F5.opPattern","COPY",BODY,{"derivedFrom":makeQuery(id+"F4.opPattern","COPY",BODY,{"derivedFrom":makeQuery(id+"F2.opPattern","COPY",BODY,{"derivedFrom":makeQuery(id+"F1.opRevolve","SWEPT_BODY",BODY,{"disambiguationData":[OSD([sQuery(id+"F0.wireOp",EDGE,"E1")])]}),"instanceName":"1"}),"instanceName":"1"}),"instanceName":"1"}),"instanceName":"1"}),"instanceName":"1"}),"instanceName":"1"});
            var Q611;
            Q611=makeQuery(id+"F11.opPattern","COPY",BODY,{"derivedFrom":makeQuery(id+"F10.opPattern","COPY",BODY,{"derivedFrom":makeQuery(id+"F7.opPattern","COPY",BODY,{"derivedFrom":makeQuery(id+"F5.opPattern","COPY",BODY,{"derivedFrom":makeQuery(id+"F4.opPattern","COPY",BODY,{"derivedFrom":makeQuery(id+"F3.opPattern","COPY",BODY,{"derivedFrom":makeQuery(id+"F2.opPattern","COPY",BODY,{"derivedFrom":makeQuery(id+"F1.opRevolve","SWEPT_BODY",BODY,{"disambiguationData":[OSD([sQuery(id+"F0.wireOp",EDGE,"E1")])]}),"instanceName":"1"}),"instanceName":"1"}),"instanceName":"1"}),"instanceName":"1"}),"instanceName":"1"}),"instanceName":"1"}),"instanceName":"1"});
            var Q612;
            Q612=makeQuery(id+"F11.opPattern","COPY",BODY,{"derivedFrom":makeQuery(id+"F10.opPattern","COPY",BODY,{"derivedFrom":makeQuery(id+"F7.opPattern","COPY",BODY,{"derivedFrom":makeQuery(id+"F6.opPattern","COPY",BODY,{"derivedFrom":makeQuery(id+"F1.opRevolve","SWEPT_BODY",BODY,{"disambiguationData":[OSD([sQuery(id+"F0.wireOp",EDGE,"E1")])]}),"instanceName":"1"}),"instanceName":"1"}),"instanceName":"1"}),"instanceName":"1"});
            var Q613;
            Q613=makeQuery(id+"F11.opPattern","COPY",BODY,{"derivedFrom":makeQuery(id+"F10.opPattern","COPY",BODY,{"derivedFrom":makeQuery(id+"F7.opPattern","COPY",BODY,{"derivedFrom":makeQuery(id+"F6.opPattern","COPY",BODY,{"derivedFrom":makeQuery(id+"F2.opPattern","COPY",BODY,{"derivedFrom":makeQuery(id+"F1.opRevolve","SWEPT_BODY",BODY,{"disambiguationData":[OSD([sQuery(id+"F0.wireOp",EDGE,"E1")])]}),"instanceName":"1"}),"instanceName":"1"}),"instanceName":"1"}),"instanceName":"1"}),"instanceName":"1"});
            var Q614;
            Q614=makeQuery(id+"F11.opPattern","COPY",BODY,{"derivedFrom":makeQuery(id+"F10.opPattern","COPY",BODY,{"derivedFrom":makeQuery(id+"F7.opPattern","COPY",BODY,{"derivedFrom":makeQuery(id+"F6.opPattern","COPY",BODY,{"derivedFrom":makeQuery(id+"F3.opPattern","COPY",BODY,{"derivedFrom":makeQuery(id+"F2.opPattern","COPY",BODY,{"derivedFrom":makeQuery(id+"F1.opRevolve","SWEPT_BODY",BODY,{"disambiguationData":[OSD([sQuery(id+"F0.wireOp",EDGE,"E1")])]}),"instanceName":"1"}),"instanceName":"1"}),"instanceName":"1"}),"instanceName":"1"}),"instanceName":"1"}),"instanceName":"1"});
            var Q615;
            Q615=makeQuery(id+"F11.opPattern","COPY",BODY,{"derivedFrom":makeQuery(id+"F10.opPattern","COPY",BODY,{"derivedFrom":makeQuery(id+"F7.opPattern","COPY",BODY,{"derivedFrom":makeQuery(id+"F6.opPattern","COPY",BODY,{"derivedFrom":makeQuery(id+"F4.opPattern","COPY",BODY,{"derivedFrom":makeQuery(id+"F1.opRevolve","SWEPT_BODY",BODY,{"disambiguationData":[OSD([sQuery(id+"F0.wireOp",EDGE,"E1")])]}),"instanceName":"1"}),"instanceName":"1"}),"instanceName":"1"}),"instanceName":"1"}),"instanceName":"1"});
            var Q616;
            Q616=makeQuery(id+"F11.opPattern","COPY",BODY,{"derivedFrom":makeQuery(id+"F10.opPattern","COPY",BODY,{"derivedFrom":makeQuery(id+"F7.opPattern","COPY",BODY,{"derivedFrom":makeQuery(id+"F6.opPattern","COPY",BODY,{"derivedFrom":makeQuery(id+"F4.opPattern","COPY",BODY,{"derivedFrom":makeQuery(id+"F2.opPattern","COPY",BODY,{"derivedFrom":makeQuery(id+"F1.opRevolve","SWEPT_BODY",BODY,{"disambiguationData":[OSD([sQuery(id+"F0.wireOp",EDGE,"E1")])]}),"instanceName":"1"}),"instanceName":"1"}),"instanceName":"1"}),"instanceName":"1"}),"instanceName":"1"}),"instanceName":"1"});
            var Q617;
            Q617=makeQuery(id+"F11.opPattern","COPY",BODY,{"derivedFrom":makeQuery(id+"F10.opPattern","COPY",BODY,{"derivedFrom":makeQuery(id+"F7.opPattern","COPY",BODY,{"derivedFrom":makeQuery(id+"F6.opPattern","COPY",BODY,{"derivedFrom":makeQuery(id+"F4.opPattern","COPY",BODY,{"derivedFrom":makeQuery(id+"F3.opPattern","COPY",BODY,{"derivedFrom":makeQuery(id+"F2.opPattern","COPY",BODY,{"derivedFrom":makeQuery(id+"F1.opRevolve","SWEPT_BODY",BODY,{"disambiguationData":[OSD([sQuery(id+"F0.wireOp",EDGE,"E1")])]}),"instanceName":"1"}),"instanceName":"1"}),"instanceName":"1"}),"instanceName":"1"}),"instanceName":"1"}),"instanceName":"1"}),"instanceName":"1"});
            var Q618;
            Q618=makeQuery(id+"F11.opPattern","COPY",BODY,{"derivedFrom":makeQuery(id+"F10.opPattern","COPY",BODY,{"derivedFrom":makeQuery(id+"F7.opPattern","COPY",BODY,{"derivedFrom":makeQuery(id+"F6.opPattern","COPY",BODY,{"derivedFrom":makeQuery(id+"F5.opPattern","COPY",BODY,{"derivedFrom":makeQuery(id+"F1.opRevolve","SWEPT_BODY",BODY,{"disambiguationData":[OSD([sQuery(id+"F0.wireOp",EDGE,"E1")])]}),"instanceName":"1"}),"instanceName":"1"}),"instanceName":"1"}),"instanceName":"1"}),"instanceName":"1"});
            var Q619;
            Q619=makeQuery(id+"F11.opPattern","COPY",BODY,{"derivedFrom":makeQuery(id+"F10.opPattern","COPY",BODY,{"derivedFrom":makeQuery(id+"F7.opPattern","COPY",BODY,{"derivedFrom":makeQuery(id+"F6.opPattern","COPY",BODY,{"derivedFrom":makeQuery(id+"F5.opPattern","COPY",BODY,{"derivedFrom":makeQuery(id+"F2.opPattern","COPY",BODY,{"derivedFrom":makeQuery(id+"F1.opRevolve","SWEPT_BODY",BODY,{"disambiguationData":[OSD([sQuery(id+"F0.wireOp",EDGE,"E1")])]}),"instanceName":"1"}),"instanceName":"1"}),"instanceName":"1"}),"instanceName":"1"}),"instanceName":"1"}),"instanceName":"1"});
            var Q620;
            Q620=makeQuery(id+"F11.opPattern","COPY",BODY,{"derivedFrom":makeQuery(id+"F10.opPattern","COPY",BODY,{"derivedFrom":makeQuery(id+"F7.opPattern","COPY",BODY,{"derivedFrom":makeQuery(id+"F6.opPattern","COPY",BODY,{"derivedFrom":makeQuery(id+"F5.opPattern","COPY",BODY,{"derivedFrom":makeQuery(id+"F3.opPattern","COPY",BODY,{"derivedFrom":makeQuery(id+"F2.opPattern","COPY",BODY,{"derivedFrom":makeQuery(id+"F1.opRevolve","SWEPT_BODY",BODY,{"disambiguationData":[OSD([sQuery(id+"F0.wireOp",EDGE,"E1")])]}),"instanceName":"1"}),"instanceName":"1"}),"instanceName":"1"}),"instanceName":"1"}),"instanceName":"1"}),"instanceName":"1"}),"instanceName":"1"});
            var Q621;
            Q621=makeQuery(id+"F11.opPattern","COPY",BODY,{"derivedFrom":makeQuery(id+"F10.opPattern","COPY",BODY,{"derivedFrom":makeQuery(id+"F7.opPattern","COPY",BODY,{"derivedFrom":makeQuery(id+"F6.opPattern","COPY",BODY,{"derivedFrom":makeQuery(id+"F5.opPattern","COPY",BODY,{"derivedFrom":makeQuery(id+"F4.opPattern","COPY",BODY,{"derivedFrom":makeQuery(id+"F1.opRevolve","SWEPT_BODY",BODY,{"disambiguationData":[OSD([sQuery(id+"F0.wireOp",EDGE,"E1")])]}),"instanceName":"1"}),"instanceName":"1"}),"instanceName":"1"}),"instanceName":"1"}),"instanceName":"1"}),"instanceName":"1"});
            var Q622;
            Q622=makeQuery(id+"F11.opPattern","COPY",BODY,{"derivedFrom":makeQuery(id+"F10.opPattern","COPY",BODY,{"derivedFrom":makeQuery(id+"F7.opPattern","COPY",BODY,{"derivedFrom":makeQuery(id+"F6.opPattern","COPY",BODY,{"derivedFrom":makeQuery(id+"F5.opPattern","COPY",BODY,{"derivedFrom":makeQuery(id+"F4.opPattern","COPY",BODY,{"derivedFrom":makeQuery(id+"F2.opPattern","COPY",BODY,{"derivedFrom":makeQuery(id+"F1.opRevolve","SWEPT_BODY",BODY,{"disambiguationData":[OSD([sQuery(id+"F0.wireOp",EDGE,"E1")])]}),"instanceName":"1"}),"instanceName":"1"}),"instanceName":"1"}),"instanceName":"1"}),"instanceName":"1"}),"instanceName":"1"}),"instanceName":"1"});
            var Q623;
            Q623=makeQuery(id+"F11.opPattern","COPY",BODY,{"derivedFrom":makeQuery(id+"F10.opPattern","COPY",BODY,{"derivedFrom":makeQuery(id+"F7.opPattern","COPY",BODY,{"derivedFrom":makeQuery(id+"F6.opPattern","COPY",BODY,{"derivedFrom":makeQuery(id+"F5.opPattern","COPY",BODY,{"derivedFrom":makeQuery(id+"F4.opPattern","COPY",BODY,{"derivedFrom":makeQuery(id+"F3.opPattern","COPY",BODY,{"derivedFrom":makeQuery(id+"F2.opPattern","COPY",BODY,{"derivedFrom":makeQuery(id+"F1.opRevolve","SWEPT_BODY",BODY,{"disambiguationData":[OSD([sQuery(id+"F0.wireOp",EDGE,"E1")])]}),"instanceName":"1"}),"instanceName":"1"}),"instanceName":"1"}),"instanceName":"1"}),"instanceName":"1"}),"instanceName":"1"}),"instanceName":"1"}),"instanceName":"1"});
            var Q624;
            Q624=makeQuery(id+"F11.opPattern","COPY",BODY,{"derivedFrom":makeQuery(id+"F10.opPattern","COPY",BODY,{"derivedFrom":makeQuery(id+"F8.opPattern","COPY",BODY,{"derivedFrom":makeQuery(id+"F1.opRevolve","SWEPT_BODY",BODY,{"disambiguationData":[OSD([sQuery(id+"F0.wireOp",EDGE,"E1")])]}),"instanceName":"1"}),"instanceName":"1"}),"instanceName":"1"});
            var Q625;
            Q625=makeQuery(id+"F11.opPattern","COPY",BODY,{"derivedFrom":makeQuery(id+"F10.opPattern","COPY",BODY,{"derivedFrom":makeQuery(id+"F8.opPattern","COPY",BODY,{"derivedFrom":makeQuery(id+"F2.opPattern","COPY",BODY,{"derivedFrom":makeQuery(id+"F1.opRevolve","SWEPT_BODY",BODY,{"disambiguationData":[OSD([sQuery(id+"F0.wireOp",EDGE,"E1")])]}),"instanceName":"1"}),"instanceName":"1"}),"instanceName":"1"}),"instanceName":"1"});
            var Q626;
            Q626=makeQuery(id+"F11.opPattern","COPY",BODY,{"derivedFrom":makeQuery(id+"F10.opPattern","COPY",BODY,{"derivedFrom":makeQuery(id+"F8.opPattern","COPY",BODY,{"derivedFrom":makeQuery(id+"F3.opPattern","COPY",BODY,{"derivedFrom":makeQuery(id+"F2.opPattern","COPY",BODY,{"derivedFrom":makeQuery(id+"F1.opRevolve","SWEPT_BODY",BODY,{"disambiguationData":[OSD([sQuery(id+"F0.wireOp",EDGE,"E1")])]}),"instanceName":"1"}),"instanceName":"1"}),"instanceName":"1"}),"instanceName":"1"}),"instanceName":"1"});
            var Q627;
            Q627=makeQuery(id+"F11.opPattern","COPY",BODY,{"derivedFrom":makeQuery(id+"F10.opPattern","COPY",BODY,{"derivedFrom":makeQuery(id+"F8.opPattern","COPY",BODY,{"derivedFrom":makeQuery(id+"F4.opPattern","COPY",BODY,{"derivedFrom":makeQuery(id+"F1.opRevolve","SWEPT_BODY",BODY,{"disambiguationData":[OSD([sQuery(id+"F0.wireOp",EDGE,"E1")])]}),"instanceName":"1"}),"instanceName":"1"}),"instanceName":"1"}),"instanceName":"1"});
            var Q628;
            Q628=makeQuery(id+"F11.opPattern","COPY",BODY,{"derivedFrom":makeQuery(id+"F10.opPattern","COPY",BODY,{"derivedFrom":makeQuery(id+"F8.opPattern","COPY",BODY,{"derivedFrom":makeQuery(id+"F4.opPattern","COPY",BODY,{"derivedFrom":makeQuery(id+"F2.opPattern","COPY",BODY,{"derivedFrom":makeQuery(id+"F1.opRevolve","SWEPT_BODY",BODY,{"disambiguationData":[OSD([sQuery(id+"F0.wireOp",EDGE,"E1")])]}),"instanceName":"1"}),"instanceName":"1"}),"instanceName":"1"}),"instanceName":"1"}),"instanceName":"1"});
            var Q629;
            Q629=makeQuery(id+"F11.opPattern","COPY",BODY,{"derivedFrom":makeQuery(id+"F10.opPattern","COPY",BODY,{"derivedFrom":makeQuery(id+"F8.opPattern","COPY",BODY,{"derivedFrom":makeQuery(id+"F4.opPattern","COPY",BODY,{"derivedFrom":makeQuery(id+"F3.opPattern","COPY",BODY,{"derivedFrom":makeQuery(id+"F2.opPattern","COPY",BODY,{"derivedFrom":makeQuery(id+"F1.opRevolve","SWEPT_BODY",BODY,{"disambiguationData":[OSD([sQuery(id+"F0.wireOp",EDGE,"E1")])]}),"instanceName":"1"}),"instanceName":"1"}),"instanceName":"1"}),"instanceName":"1"}),"instanceName":"1"}),"instanceName":"1"});
            var Q630;
            Q630=makeQuery(id+"F11.opPattern","COPY",BODY,{"derivedFrom":makeQuery(id+"F10.opPattern","COPY",BODY,{"derivedFrom":makeQuery(id+"F8.opPattern","COPY",BODY,{"derivedFrom":makeQuery(id+"F5.opPattern","COPY",BODY,{"derivedFrom":makeQuery(id+"F1.opRevolve","SWEPT_BODY",BODY,{"disambiguationData":[OSD([sQuery(id+"F0.wireOp",EDGE,"E1")])]}),"instanceName":"1"}),"instanceName":"1"}),"instanceName":"1"}),"instanceName":"1"});
            var Q631;
            Q631=makeQuery(id+"F11.opPattern","COPY",BODY,{"derivedFrom":makeQuery(id+"F10.opPattern","COPY",BODY,{"derivedFrom":makeQuery(id+"F8.opPattern","COPY",BODY,{"derivedFrom":makeQuery(id+"F5.opPattern","COPY",BODY,{"derivedFrom":makeQuery(id+"F2.opPattern","COPY",BODY,{"derivedFrom":makeQuery(id+"F1.opRevolve","SWEPT_BODY",BODY,{"disambiguationData":[OSD([sQuery(id+"F0.wireOp",EDGE,"E1")])]}),"instanceName":"1"}),"instanceName":"1"}),"instanceName":"1"}),"instanceName":"1"}),"instanceName":"1"});
            var Q632;
            Q632=makeQuery(id+"F11.opPattern","COPY",BODY,{"derivedFrom":makeQuery(id+"F10.opPattern","COPY",BODY,{"derivedFrom":makeQuery(id+"F8.opPattern","COPY",BODY,{"derivedFrom":makeQuery(id+"F5.opPattern","COPY",BODY,{"derivedFrom":makeQuery(id+"F3.opPattern","COPY",BODY,{"derivedFrom":makeQuery(id+"F2.opPattern","COPY",BODY,{"derivedFrom":makeQuery(id+"F1.opRevolve","SWEPT_BODY",BODY,{"disambiguationData":[OSD([sQuery(id+"F0.wireOp",EDGE,"E1")])]}),"instanceName":"1"}),"instanceName":"1"}),"instanceName":"1"}),"instanceName":"1"}),"instanceName":"1"}),"instanceName":"1"});
            var Q633;
            Q633=makeQuery(id+"F11.opPattern","COPY",BODY,{"derivedFrom":makeQuery(id+"F10.opPattern","COPY",BODY,{"derivedFrom":makeQuery(id+"F8.opPattern","COPY",BODY,{"derivedFrom":makeQuery(id+"F5.opPattern","COPY",BODY,{"derivedFrom":makeQuery(id+"F4.opPattern","COPY",BODY,{"derivedFrom":makeQuery(id+"F1.opRevolve","SWEPT_BODY",BODY,{"disambiguationData":[OSD([sQuery(id+"F0.wireOp",EDGE,"E1")])]}),"instanceName":"1"}),"instanceName":"1"}),"instanceName":"1"}),"instanceName":"1"}),"instanceName":"1"});
            var Q634;
            Q634=makeQuery(id+"F11.opPattern","COPY",BODY,{"derivedFrom":makeQuery(id+"F10.opPattern","COPY",BODY,{"derivedFrom":makeQuery(id+"F8.opPattern","COPY",BODY,{"derivedFrom":makeQuery(id+"F5.opPattern","COPY",BODY,{"derivedFrom":makeQuery(id+"F4.opPattern","COPY",BODY,{"derivedFrom":makeQuery(id+"F2.opPattern","COPY",BODY,{"derivedFrom":makeQuery(id+"F1.opRevolve","SWEPT_BODY",BODY,{"disambiguationData":[OSD([sQuery(id+"F0.wireOp",EDGE,"E1")])]}),"instanceName":"1"}),"instanceName":"1"}),"instanceName":"1"}),"instanceName":"1"}),"instanceName":"1"}),"instanceName":"1"});
            var Q635;
            Q635=makeQuery(id+"F11.opPattern","COPY",BODY,{"derivedFrom":makeQuery(id+"F10.opPattern","COPY",BODY,{"derivedFrom":makeQuery(id+"F8.opPattern","COPY",BODY,{"derivedFrom":makeQuery(id+"F5.opPattern","COPY",BODY,{"derivedFrom":makeQuery(id+"F4.opPattern","COPY",BODY,{"derivedFrom":makeQuery(id+"F3.opPattern","COPY",BODY,{"derivedFrom":makeQuery(id+"F2.opPattern","COPY",BODY,{"derivedFrom":makeQuery(id+"F1.opRevolve","SWEPT_BODY",BODY,{"disambiguationData":[OSD([sQuery(id+"F0.wireOp",EDGE,"E1")])]}),"instanceName":"1"}),"instanceName":"1"}),"instanceName":"1"}),"instanceName":"1"}),"instanceName":"1"}),"instanceName":"1"}),"instanceName":"1"});
            var Q636;
            Q636=makeQuery(id+"F11.opPattern","COPY",BODY,{"derivedFrom":makeQuery(id+"F10.opPattern","COPY",BODY,{"derivedFrom":makeQuery(id+"F8.opPattern","COPY",BODY,{"derivedFrom":makeQuery(id+"F6.opPattern","COPY",BODY,{"derivedFrom":makeQuery(id+"F1.opRevolve","SWEPT_BODY",BODY,{"disambiguationData":[OSD([sQuery(id+"F0.wireOp",EDGE,"E1")])]}),"instanceName":"1"}),"instanceName":"1"}),"instanceName":"1"}),"instanceName":"1"});
            var Q637;
            Q637=makeQuery(id+"F11.opPattern","COPY",BODY,{"derivedFrom":makeQuery(id+"F10.opPattern","COPY",BODY,{"derivedFrom":makeQuery(id+"F8.opPattern","COPY",BODY,{"derivedFrom":makeQuery(id+"F6.opPattern","COPY",BODY,{"derivedFrom":makeQuery(id+"F2.opPattern","COPY",BODY,{"derivedFrom":makeQuery(id+"F1.opRevolve","SWEPT_BODY",BODY,{"disambiguationData":[OSD([sQuery(id+"F0.wireOp",EDGE,"E1")])]}),"instanceName":"1"}),"instanceName":"1"}),"instanceName":"1"}),"instanceName":"1"}),"instanceName":"1"});
            var Q638;
            Q638=makeQuery(id+"F11.opPattern","COPY",BODY,{"derivedFrom":makeQuery(id+"F10.opPattern","COPY",BODY,{"derivedFrom":makeQuery(id+"F8.opPattern","COPY",BODY,{"derivedFrom":makeQuery(id+"F6.opPattern","COPY",BODY,{"derivedFrom":makeQuery(id+"F3.opPattern","COPY",BODY,{"derivedFrom":makeQuery(id+"F2.opPattern","COPY",BODY,{"derivedFrom":makeQuery(id+"F1.opRevolve","SWEPT_BODY",BODY,{"disambiguationData":[OSD([sQuery(id+"F0.wireOp",EDGE,"E1")])]}),"instanceName":"1"}),"instanceName":"1"}),"instanceName":"1"}),"instanceName":"1"}),"instanceName":"1"}),"instanceName":"1"});
            var Q639;
            Q639=makeQuery(id+"F11.opPattern","COPY",BODY,{"derivedFrom":makeQuery(id+"F10.opPattern","COPY",BODY,{"derivedFrom":makeQuery(id+"F8.opPattern","COPY",BODY,{"derivedFrom":makeQuery(id+"F6.opPattern","COPY",BODY,{"derivedFrom":makeQuery(id+"F4.opPattern","COPY",BODY,{"derivedFrom":makeQuery(id+"F1.opRevolve","SWEPT_BODY",BODY,{"disambiguationData":[OSD([sQuery(id+"F0.wireOp",EDGE,"E1")])]}),"instanceName":"1"}),"instanceName":"1"}),"instanceName":"1"}),"instanceName":"1"}),"instanceName":"1"});
            var Q640;
            Q640=makeQuery(id+"F11.opPattern","COPY",BODY,{"derivedFrom":makeQuery(id+"F10.opPattern","COPY",BODY,{"derivedFrom":makeQuery(id+"F8.opPattern","COPY",BODY,{"derivedFrom":makeQuery(id+"F6.opPattern","COPY",BODY,{"derivedFrom":makeQuery(id+"F4.opPattern","COPY",BODY,{"derivedFrom":makeQuery(id+"F2.opPattern","COPY",BODY,{"derivedFrom":makeQuery(id+"F1.opRevolve","SWEPT_BODY",BODY,{"disambiguationData":[OSD([sQuery(id+"F0.wireOp",EDGE,"E1")])]}),"instanceName":"1"}),"instanceName":"1"}),"instanceName":"1"}),"instanceName":"1"}),"instanceName":"1"}),"instanceName":"1"});
            var Q641;
            Q641=makeQuery(id+"F11.opPattern","COPY",BODY,{"derivedFrom":makeQuery(id+"F10.opPattern","COPY",BODY,{"derivedFrom":makeQuery(id+"F8.opPattern","COPY",BODY,{"derivedFrom":makeQuery(id+"F6.opPattern","COPY",BODY,{"derivedFrom":makeQuery(id+"F4.opPattern","COPY",BODY,{"derivedFrom":makeQuery(id+"F3.opPattern","COPY",BODY,{"derivedFrom":makeQuery(id+"F2.opPattern","COPY",BODY,{"derivedFrom":makeQuery(id+"F1.opRevolve","SWEPT_BODY",BODY,{"disambiguationData":[OSD([sQuery(id+"F0.wireOp",EDGE,"E1")])]}),"instanceName":"1"}),"instanceName":"1"}),"instanceName":"1"}),"instanceName":"1"}),"instanceName":"1"}),"instanceName":"1"}),"instanceName":"1"});
            var Q642;
            Q642=makeQuery(id+"F11.opPattern","COPY",BODY,{"derivedFrom":makeQuery(id+"F10.opPattern","COPY",BODY,{"derivedFrom":makeQuery(id+"F8.opPattern","COPY",BODY,{"derivedFrom":makeQuery(id+"F6.opPattern","COPY",BODY,{"derivedFrom":makeQuery(id+"F5.opPattern","COPY",BODY,{"derivedFrom":makeQuery(id+"F1.opRevolve","SWEPT_BODY",BODY,{"disambiguationData":[OSD([sQuery(id+"F0.wireOp",EDGE,"E1")])]}),"instanceName":"1"}),"instanceName":"1"}),"instanceName":"1"}),"instanceName":"1"}),"instanceName":"1"});
            var Q643;
            Q643=makeQuery(id+"F11.opPattern","COPY",BODY,{"derivedFrom":makeQuery(id+"F10.opPattern","COPY",BODY,{"derivedFrom":makeQuery(id+"F8.opPattern","COPY",BODY,{"derivedFrom":makeQuery(id+"F6.opPattern","COPY",BODY,{"derivedFrom":makeQuery(id+"F5.opPattern","COPY",BODY,{"derivedFrom":makeQuery(id+"F2.opPattern","COPY",BODY,{"derivedFrom":makeQuery(id+"F1.opRevolve","SWEPT_BODY",BODY,{"disambiguationData":[OSD([sQuery(id+"F0.wireOp",EDGE,"E1")])]}),"instanceName":"1"}),"instanceName":"1"}),"instanceName":"1"}),"instanceName":"1"}),"instanceName":"1"}),"instanceName":"1"});
            var Q644;
            Q644=makeQuery(id+"F11.opPattern","COPY",BODY,{"derivedFrom":makeQuery(id+"F10.opPattern","COPY",BODY,{"derivedFrom":makeQuery(id+"F8.opPattern","COPY",BODY,{"derivedFrom":makeQuery(id+"F6.opPattern","COPY",BODY,{"derivedFrom":makeQuery(id+"F5.opPattern","COPY",BODY,{"derivedFrom":makeQuery(id+"F3.opPattern","COPY",BODY,{"derivedFrom":makeQuery(id+"F2.opPattern","COPY",BODY,{"derivedFrom":makeQuery(id+"F1.opRevolve","SWEPT_BODY",BODY,{"disambiguationData":[OSD([sQuery(id+"F0.wireOp",EDGE,"E1")])]}),"instanceName":"1"}),"instanceName":"1"}),"instanceName":"1"}),"instanceName":"1"}),"instanceName":"1"}),"instanceName":"1"}),"instanceName":"1"});
            var Q645;
            Q645=makeQuery(id+"F11.opPattern","COPY",BODY,{"derivedFrom":makeQuery(id+"F10.opPattern","COPY",BODY,{"derivedFrom":makeQuery(id+"F8.opPattern","COPY",BODY,{"derivedFrom":makeQuery(id+"F6.opPattern","COPY",BODY,{"derivedFrom":makeQuery(id+"F5.opPattern","COPY",BODY,{"derivedFrom":makeQuery(id+"F4.opPattern","COPY",BODY,{"derivedFrom":makeQuery(id+"F1.opRevolve","SWEPT_BODY",BODY,{"disambiguationData":[OSD([sQuery(id+"F0.wireOp",EDGE,"E1")])]}),"instanceName":"1"}),"instanceName":"1"}),"instanceName":"1"}),"instanceName":"1"}),"instanceName":"1"}),"instanceName":"1"});
            var Q646;
            Q646=makeQuery(id+"F11.opPattern","COPY",BODY,{"derivedFrom":makeQuery(id+"F10.opPattern","COPY",BODY,{"derivedFrom":makeQuery(id+"F8.opPattern","COPY",BODY,{"derivedFrom":makeQuery(id+"F6.opPattern","COPY",BODY,{"derivedFrom":makeQuery(id+"F5.opPattern","COPY",BODY,{"derivedFrom":makeQuery(id+"F4.opPattern","COPY",BODY,{"derivedFrom":makeQuery(id+"F2.opPattern","COPY",BODY,{"derivedFrom":makeQuery(id+"F1.opRevolve","SWEPT_BODY",BODY,{"disambiguationData":[OSD([sQuery(id+"F0.wireOp",EDGE,"E1")])]}),"instanceName":"1"}),"instanceName":"1"}),"instanceName":"1"}),"instanceName":"1"}),"instanceName":"1"}),"instanceName":"1"}),"instanceName":"1"});
            var Q647;
            Q647=makeQuery(id+"F11.opPattern","COPY",BODY,{"derivedFrom":makeQuery(id+"F10.opPattern","COPY",BODY,{"derivedFrom":makeQuery(id+"F8.opPattern","COPY",BODY,{"derivedFrom":makeQuery(id+"F6.opPattern","COPY",BODY,{"derivedFrom":makeQuery(id+"F5.opPattern","COPY",BODY,{"derivedFrom":makeQuery(id+"F4.opPattern","COPY",BODY,{"derivedFrom":makeQuery(id+"F3.opPattern","COPY",BODY,{"derivedFrom":makeQuery(id+"F2.opPattern","COPY",BODY,{"derivedFrom":makeQuery(id+"F1.opRevolve","SWEPT_BODY",BODY,{"disambiguationData":[OSD([sQuery(id+"F0.wireOp",EDGE,"E1")])]}),"instanceName":"1"}),"instanceName":"1"}),"instanceName":"1"}),"instanceName":"1"}),"instanceName":"1"}),"instanceName":"1"}),"instanceName":"1"}),"instanceName":"1"});
            var Q648;
            Q648=makeQuery(id+"F11.opPattern","COPY",BODY,{"derivedFrom":makeQuery(id+"F10.opPattern","COPY",BODY,{"derivedFrom":makeQuery(id+"F8.opPattern","COPY",BODY,{"derivedFrom":makeQuery(id+"F7.opPattern","COPY",BODY,{"derivedFrom":makeQuery(id+"F1.opRevolve","SWEPT_BODY",BODY,{"disambiguationData":[OSD([sQuery(id+"F0.wireOp",EDGE,"E1")])]}),"instanceName":"1"}),"instanceName":"1"}),"instanceName":"1"}),"instanceName":"1"});
            var Q649;
            Q649=makeQuery(id+"F11.opPattern","COPY",BODY,{"derivedFrom":makeQuery(id+"F10.opPattern","COPY",BODY,{"derivedFrom":makeQuery(id+"F8.opPattern","COPY",BODY,{"derivedFrom":makeQuery(id+"F7.opPattern","COPY",BODY,{"derivedFrom":makeQuery(id+"F2.opPattern","COPY",BODY,{"derivedFrom":makeQuery(id+"F1.opRevolve","SWEPT_BODY",BODY,{"disambiguationData":[OSD([sQuery(id+"F0.wireOp",EDGE,"E1")])]}),"instanceName":"1"}),"instanceName":"1"}),"instanceName":"1"}),"instanceName":"1"}),"instanceName":"1"});
            var Q650;
            Q650=makeQuery(id+"F11.opPattern","COPY",BODY,{"derivedFrom":makeQuery(id+"F10.opPattern","COPY",BODY,{"derivedFrom":makeQuery(id+"F8.opPattern","COPY",BODY,{"derivedFrom":makeQuery(id+"F7.opPattern","COPY",BODY,{"derivedFrom":makeQuery(id+"F3.opPattern","COPY",BODY,{"derivedFrom":makeQuery(id+"F2.opPattern","COPY",BODY,{"derivedFrom":makeQuery(id+"F1.opRevolve","SWEPT_BODY",BODY,{"disambiguationData":[OSD([sQuery(id+"F0.wireOp",EDGE,"E1")])]}),"instanceName":"1"}),"instanceName":"1"}),"instanceName":"1"}),"instanceName":"1"}),"instanceName":"1"}),"instanceName":"1"});
            var Q651;
            Q651=makeQuery(id+"F11.opPattern","COPY",BODY,{"derivedFrom":makeQuery(id+"F10.opPattern","COPY",BODY,{"derivedFrom":makeQuery(id+"F8.opPattern","COPY",BODY,{"derivedFrom":makeQuery(id+"F7.opPattern","COPY",BODY,{"derivedFrom":makeQuery(id+"F4.opPattern","COPY",BODY,{"derivedFrom":makeQuery(id+"F1.opRevolve","SWEPT_BODY",BODY,{"disambiguationData":[OSD([sQuery(id+"F0.wireOp",EDGE,"E1")])]}),"instanceName":"1"}),"instanceName":"1"}),"instanceName":"1"}),"instanceName":"1"}),"instanceName":"1"});
            var Q652;
            Q652=makeQuery(id+"F11.opPattern","COPY",BODY,{"derivedFrom":makeQuery(id+"F10.opPattern","COPY",BODY,{"derivedFrom":makeQuery(id+"F8.opPattern","COPY",BODY,{"derivedFrom":makeQuery(id+"F7.opPattern","COPY",BODY,{"derivedFrom":makeQuery(id+"F4.opPattern","COPY",BODY,{"derivedFrom":makeQuery(id+"F2.opPattern","COPY",BODY,{"derivedFrom":makeQuery(id+"F1.opRevolve","SWEPT_BODY",BODY,{"disambiguationData":[OSD([sQuery(id+"F0.wireOp",EDGE,"E1")])]}),"instanceName":"1"}),"instanceName":"1"}),"instanceName":"1"}),"instanceName":"1"}),"instanceName":"1"}),"instanceName":"1"});
            var Q653;
            Q653=makeQuery(id+"F11.opPattern","COPY",BODY,{"derivedFrom":makeQuery(id+"F10.opPattern","COPY",BODY,{"derivedFrom":makeQuery(id+"F8.opPattern","COPY",BODY,{"derivedFrom":makeQuery(id+"F7.opPattern","COPY",BODY,{"derivedFrom":makeQuery(id+"F4.opPattern","COPY",BODY,{"derivedFrom":makeQuery(id+"F3.opPattern","COPY",BODY,{"derivedFrom":makeQuery(id+"F2.opPattern","COPY",BODY,{"derivedFrom":makeQuery(id+"F1.opRevolve","SWEPT_BODY",BODY,{"disambiguationData":[OSD([sQuery(id+"F0.wireOp",EDGE,"E1")])]}),"instanceName":"1"}),"instanceName":"1"}),"instanceName":"1"}),"instanceName":"1"}),"instanceName":"1"}),"instanceName":"1"}),"instanceName":"1"});
            var Q654;
            Q654=makeQuery(id+"F11.opPattern","COPY",BODY,{"derivedFrom":makeQuery(id+"F10.opPattern","COPY",BODY,{"derivedFrom":makeQuery(id+"F8.opPattern","COPY",BODY,{"derivedFrom":makeQuery(id+"F7.opPattern","COPY",BODY,{"derivedFrom":makeQuery(id+"F5.opPattern","COPY",BODY,{"derivedFrom":makeQuery(id+"F1.opRevolve","SWEPT_BODY",BODY,{"disambiguationData":[OSD([sQuery(id+"F0.wireOp",EDGE,"E1")])]}),"instanceName":"1"}),"instanceName":"1"}),"instanceName":"1"}),"instanceName":"1"}),"instanceName":"1"});
            var Q655;
            Q655=makeQuery(id+"F11.opPattern","COPY",BODY,{"derivedFrom":makeQuery(id+"F10.opPattern","COPY",BODY,{"derivedFrom":makeQuery(id+"F8.opPattern","COPY",BODY,{"derivedFrom":makeQuery(id+"F7.opPattern","COPY",BODY,{"derivedFrom":makeQuery(id+"F5.opPattern","COPY",BODY,{"derivedFrom":makeQuery(id+"F2.opPattern","COPY",BODY,{"derivedFrom":makeQuery(id+"F1.opRevolve","SWEPT_BODY",BODY,{"disambiguationData":[OSD([sQuery(id+"F0.wireOp",EDGE,"E1")])]}),"instanceName":"1"}),"instanceName":"1"}),"instanceName":"1"}),"instanceName":"1"}),"instanceName":"1"}),"instanceName":"1"});
            var Q656;
            Q656=makeQuery(id+"F11.opPattern","COPY",BODY,{"derivedFrom":makeQuery(id+"F10.opPattern","COPY",BODY,{"derivedFrom":makeQuery(id+"F8.opPattern","COPY",BODY,{"derivedFrom":makeQuery(id+"F7.opPattern","COPY",BODY,{"derivedFrom":makeQuery(id+"F5.opPattern","COPY",BODY,{"derivedFrom":makeQuery(id+"F3.opPattern","COPY",BODY,{"derivedFrom":makeQuery(id+"F2.opPattern","COPY",BODY,{"derivedFrom":makeQuery(id+"F1.opRevolve","SWEPT_BODY",BODY,{"disambiguationData":[OSD([sQuery(id+"F0.wireOp",EDGE,"E1")])]}),"instanceName":"1"}),"instanceName":"1"}),"instanceName":"1"}),"instanceName":"1"}),"instanceName":"1"}),"instanceName":"1"}),"instanceName":"1"});
            var Q657;
            Q657=makeQuery(id+"F11.opPattern","COPY",BODY,{"derivedFrom":makeQuery(id+"F10.opPattern","COPY",BODY,{"derivedFrom":makeQuery(id+"F8.opPattern","COPY",BODY,{"derivedFrom":makeQuery(id+"F7.opPattern","COPY",BODY,{"derivedFrom":makeQuery(id+"F5.opPattern","COPY",BODY,{"derivedFrom":makeQuery(id+"F4.opPattern","COPY",BODY,{"derivedFrom":makeQuery(id+"F1.opRevolve","SWEPT_BODY",BODY,{"disambiguationData":[OSD([sQuery(id+"F0.wireOp",EDGE,"E1")])]}),"instanceName":"1"}),"instanceName":"1"}),"instanceName":"1"}),"instanceName":"1"}),"instanceName":"1"}),"instanceName":"1"});
            var Q658;
            Q658=makeQuery(id+"F11.opPattern","COPY",BODY,{"derivedFrom":makeQuery(id+"F10.opPattern","COPY",BODY,{"derivedFrom":makeQuery(id+"F8.opPattern","COPY",BODY,{"derivedFrom":makeQuery(id+"F7.opPattern","COPY",BODY,{"derivedFrom":makeQuery(id+"F5.opPattern","COPY",BODY,{"derivedFrom":makeQuery(id+"F4.opPattern","COPY",BODY,{"derivedFrom":makeQuery(id+"F2.opPattern","COPY",BODY,{"derivedFrom":makeQuery(id+"F1.opRevolve","SWEPT_BODY",BODY,{"disambiguationData":[OSD([sQuery(id+"F0.wireOp",EDGE,"E1")])]}),"instanceName":"1"}),"instanceName":"1"}),"instanceName":"1"}),"instanceName":"1"}),"instanceName":"1"}),"instanceName":"1"}),"instanceName":"1"});
            var Q659;
            Q659=makeQuery(id+"F11.opPattern","COPY",BODY,{"derivedFrom":makeQuery(id+"F10.opPattern","COPY",BODY,{"derivedFrom":makeQuery(id+"F8.opPattern","COPY",BODY,{"derivedFrom":makeQuery(id+"F7.opPattern","COPY",BODY,{"derivedFrom":makeQuery(id+"F5.opPattern","COPY",BODY,{"derivedFrom":makeQuery(id+"F4.opPattern","COPY",BODY,{"derivedFrom":makeQuery(id+"F3.opPattern","COPY",BODY,{"derivedFrom":makeQuery(id+"F2.opPattern","COPY",BODY,{"derivedFrom":makeQuery(id+"F1.opRevolve","SWEPT_BODY",BODY,{"disambiguationData":[OSD([sQuery(id+"F0.wireOp",EDGE,"E1")])]}),"instanceName":"1"}),"instanceName":"1"}),"instanceName":"1"}),"instanceName":"1"}),"instanceName":"1"}),"instanceName":"1"}),"instanceName":"1"}),"instanceName":"1"});
            var Q660;
            Q660=makeQuery(id+"F11.opPattern","COPY",BODY,{"derivedFrom":makeQuery(id+"F10.opPattern","COPY",BODY,{"derivedFrom":makeQuery(id+"F8.opPattern","COPY",BODY,{"derivedFrom":makeQuery(id+"F7.opPattern","COPY",BODY,{"derivedFrom":makeQuery(id+"F6.opPattern","COPY",BODY,{"derivedFrom":makeQuery(id+"F1.opRevolve","SWEPT_BODY",BODY,{"disambiguationData":[OSD([sQuery(id+"F0.wireOp",EDGE,"E1")])]}),"instanceName":"1"}),"instanceName":"1"}),"instanceName":"1"}),"instanceName":"1"}),"instanceName":"1"});
            var Q661;
            Q661=makeQuery(id+"F11.opPattern","COPY",BODY,{"derivedFrom":makeQuery(id+"F10.opPattern","COPY",BODY,{"derivedFrom":makeQuery(id+"F8.opPattern","COPY",BODY,{"derivedFrom":makeQuery(id+"F7.opPattern","COPY",BODY,{"derivedFrom":makeQuery(id+"F6.opPattern","COPY",BODY,{"derivedFrom":makeQuery(id+"F2.opPattern","COPY",BODY,{"derivedFrom":makeQuery(id+"F1.opRevolve","SWEPT_BODY",BODY,{"disambiguationData":[OSD([sQuery(id+"F0.wireOp",EDGE,"E1")])]}),"instanceName":"1"}),"instanceName":"1"}),"instanceName":"1"}),"instanceName":"1"}),"instanceName":"1"}),"instanceName":"1"});
            var Q662;
            Q662=makeQuery(id+"F11.opPattern","COPY",BODY,{"derivedFrom":makeQuery(id+"F10.opPattern","COPY",BODY,{"derivedFrom":makeQuery(id+"F8.opPattern","COPY",BODY,{"derivedFrom":makeQuery(id+"F7.opPattern","COPY",BODY,{"derivedFrom":makeQuery(id+"F6.opPattern","COPY",BODY,{"derivedFrom":makeQuery(id+"F3.opPattern","COPY",BODY,{"derivedFrom":makeQuery(id+"F2.opPattern","COPY",BODY,{"derivedFrom":makeQuery(id+"F1.opRevolve","SWEPT_BODY",BODY,{"disambiguationData":[OSD([sQuery(id+"F0.wireOp",EDGE,"E1")])]}),"instanceName":"1"}),"instanceName":"1"}),"instanceName":"1"}),"instanceName":"1"}),"instanceName":"1"}),"instanceName":"1"}),"instanceName":"1"});
            var Q663;
            Q663=makeQuery(id+"F11.opPattern","COPY",BODY,{"derivedFrom":makeQuery(id+"F10.opPattern","COPY",BODY,{"derivedFrom":makeQuery(id+"F8.opPattern","COPY",BODY,{"derivedFrom":makeQuery(id+"F7.opPattern","COPY",BODY,{"derivedFrom":makeQuery(id+"F6.opPattern","COPY",BODY,{"derivedFrom":makeQuery(id+"F4.opPattern","COPY",BODY,{"derivedFrom":makeQuery(id+"F1.opRevolve","SWEPT_BODY",BODY,{"disambiguationData":[OSD([sQuery(id+"F0.wireOp",EDGE,"E1")])]}),"instanceName":"1"}),"instanceName":"1"}),"instanceName":"1"}),"instanceName":"1"}),"instanceName":"1"}),"instanceName":"1"});
            var Q664;
            Q664=makeQuery(id+"F11.opPattern","COPY",BODY,{"derivedFrom":makeQuery(id+"F10.opPattern","COPY",BODY,{"derivedFrom":makeQuery(id+"F8.opPattern","COPY",BODY,{"derivedFrom":makeQuery(id+"F7.opPattern","COPY",BODY,{"derivedFrom":makeQuery(id+"F6.opPattern","COPY",BODY,{"derivedFrom":makeQuery(id+"F4.opPattern","COPY",BODY,{"derivedFrom":makeQuery(id+"F2.opPattern","COPY",BODY,{"derivedFrom":makeQuery(id+"F1.opRevolve","SWEPT_BODY",BODY,{"disambiguationData":[OSD([sQuery(id+"F0.wireOp",EDGE,"E1")])]}),"instanceName":"1"}),"instanceName":"1"}),"instanceName":"1"}),"instanceName":"1"}),"instanceName":"1"}),"instanceName":"1"}),"instanceName":"1"});
            var Q665;
            Q665=makeQuery(id+"F11.opPattern","COPY",BODY,{"derivedFrom":makeQuery(id+"F10.opPattern","COPY",BODY,{"derivedFrom":makeQuery(id+"F8.opPattern","COPY",BODY,{"derivedFrom":makeQuery(id+"F7.opPattern","COPY",BODY,{"derivedFrom":makeQuery(id+"F6.opPattern","COPY",BODY,{"derivedFrom":makeQuery(id+"F4.opPattern","COPY",BODY,{"derivedFrom":makeQuery(id+"F3.opPattern","COPY",BODY,{"derivedFrom":makeQuery(id+"F2.opPattern","COPY",BODY,{"derivedFrom":makeQuery(id+"F1.opRevolve","SWEPT_BODY",BODY,{"disambiguationData":[OSD([sQuery(id+"F0.wireOp",EDGE,"E1")])]}),"instanceName":"1"}),"instanceName":"1"}),"instanceName":"1"}),"instanceName":"1"}),"instanceName":"1"}),"instanceName":"1"}),"instanceName":"1"}),"instanceName":"1"});
            var Q666;
            Q666=makeQuery(id+"F11.opPattern","COPY",BODY,{"derivedFrom":makeQuery(id+"F10.opPattern","COPY",BODY,{"derivedFrom":makeQuery(id+"F8.opPattern","COPY",BODY,{"derivedFrom":makeQuery(id+"F7.opPattern","COPY",BODY,{"derivedFrom":makeQuery(id+"F6.opPattern","COPY",BODY,{"derivedFrom":makeQuery(id+"F5.opPattern","COPY",BODY,{"derivedFrom":makeQuery(id+"F1.opRevolve","SWEPT_BODY",BODY,{"disambiguationData":[OSD([sQuery(id+"F0.wireOp",EDGE,"E1")])]}),"instanceName":"1"}),"instanceName":"1"}),"instanceName":"1"}),"instanceName":"1"}),"instanceName":"1"}),"instanceName":"1"});
            var Q667;
            Q667=makeQuery(id+"F11.opPattern","COPY",BODY,{"derivedFrom":makeQuery(id+"F10.opPattern","COPY",BODY,{"derivedFrom":makeQuery(id+"F8.opPattern","COPY",BODY,{"derivedFrom":makeQuery(id+"F7.opPattern","COPY",BODY,{"derivedFrom":makeQuery(id+"F6.opPattern","COPY",BODY,{"derivedFrom":makeQuery(id+"F5.opPattern","COPY",BODY,{"derivedFrom":makeQuery(id+"F2.opPattern","COPY",BODY,{"derivedFrom":makeQuery(id+"F1.opRevolve","SWEPT_BODY",BODY,{"disambiguationData":[OSD([sQuery(id+"F0.wireOp",EDGE,"E1")])]}),"instanceName":"1"}),"instanceName":"1"}),"instanceName":"1"}),"instanceName":"1"}),"instanceName":"1"}),"instanceName":"1"}),"instanceName":"1"});
            var Q668;
            Q668=makeQuery(id+"F11.opPattern","COPY",BODY,{"derivedFrom":makeQuery(id+"F10.opPattern","COPY",BODY,{"derivedFrom":makeQuery(id+"F8.opPattern","COPY",BODY,{"derivedFrom":makeQuery(id+"F7.opPattern","COPY",BODY,{"derivedFrom":makeQuery(id+"F6.opPattern","COPY",BODY,{"derivedFrom":makeQuery(id+"F5.opPattern","COPY",BODY,{"derivedFrom":makeQuery(id+"F3.opPattern","COPY",BODY,{"derivedFrom":makeQuery(id+"F2.opPattern","COPY",BODY,{"derivedFrom":makeQuery(id+"F1.opRevolve","SWEPT_BODY",BODY,{"disambiguationData":[OSD([sQuery(id+"F0.wireOp",EDGE,"E1")])]}),"instanceName":"1"}),"instanceName":"1"}),"instanceName":"1"}),"instanceName":"1"}),"instanceName":"1"}),"instanceName":"1"}),"instanceName":"1"}),"instanceName":"1"});
            var Q669;
            Q669=makeQuery(id+"F11.opPattern","COPY",BODY,{"derivedFrom":makeQuery(id+"F10.opPattern","COPY",BODY,{"derivedFrom":makeQuery(id+"F8.opPattern","COPY",BODY,{"derivedFrom":makeQuery(id+"F7.opPattern","COPY",BODY,{"derivedFrom":makeQuery(id+"F6.opPattern","COPY",BODY,{"derivedFrom":makeQuery(id+"F5.opPattern","COPY",BODY,{"derivedFrom":makeQuery(id+"F4.opPattern","COPY",BODY,{"derivedFrom":makeQuery(id+"F1.opRevolve","SWEPT_BODY",BODY,{"disambiguationData":[OSD([sQuery(id+"F0.wireOp",EDGE,"E1")])]}),"instanceName":"1"}),"instanceName":"1"}),"instanceName":"1"}),"instanceName":"1"}),"instanceName":"1"}),"instanceName":"1"}),"instanceName":"1"});
            var Q670;
            Q670=makeQuery(id+"F11.opPattern","COPY",BODY,{"derivedFrom":makeQuery(id+"F10.opPattern","COPY",BODY,{"derivedFrom":makeQuery(id+"F8.opPattern","COPY",BODY,{"derivedFrom":makeQuery(id+"F7.opPattern","COPY",BODY,{"derivedFrom":makeQuery(id+"F6.opPattern","COPY",BODY,{"derivedFrom":makeQuery(id+"F5.opPattern","COPY",BODY,{"derivedFrom":makeQuery(id+"F4.opPattern","COPY",BODY,{"derivedFrom":makeQuery(id+"F2.opPattern","COPY",BODY,{"derivedFrom":makeQuery(id+"F1.opRevolve","SWEPT_BODY",BODY,{"disambiguationData":[OSD([sQuery(id+"F0.wireOp",EDGE,"E1")])]}),"instanceName":"1"}),"instanceName":"1"}),"instanceName":"1"}),"instanceName":"1"}),"instanceName":"1"}),"instanceName":"1"}),"instanceName":"1"}),"instanceName":"1"});
            var Q671;
            Q671=makeQuery(id+"F11.opPattern","COPY",BODY,{"derivedFrom":makeQuery(id+"F10.opPattern","COPY",BODY,{"derivedFrom":makeQuery(id+"F8.opPattern","COPY",BODY,{"derivedFrom":makeQuery(id+"F7.opPattern","COPY",BODY,{"derivedFrom":makeQuery(id+"F6.opPattern","COPY",BODY,{"derivedFrom":makeQuery(id+"F5.opPattern","COPY",BODY,{"derivedFrom":makeQuery(id+"F4.opPattern","COPY",BODY,{"derivedFrom":makeQuery(id+"F3.opPattern","COPY",BODY,{"derivedFrom":makeQuery(id+"F2.opPattern","COPY",BODY,{"derivedFrom":makeQuery(id+"F1.opRevolve","SWEPT_BODY",BODY,{"disambiguationData":[OSD([sQuery(id+"F0.wireOp",EDGE,"E1")])]}),"instanceName":"1"}),"instanceName":"1"}),"instanceName":"1"}),"instanceName":"1"}),"instanceName":"1"}),"instanceName":"1"}),"instanceName":"1"}),"instanceName":"1"}),"instanceName":"1"});
            var Q672;
            Q672=makeQuery(id+"F11.opPattern","COPY",BODY,{"derivedFrom":makeQuery(id+"F10.opPattern","COPY",BODY,{"derivedFrom":makeQuery(id+"F9.opPattern","COPY",BODY,{"derivedFrom":makeQuery(id+"F1.opRevolve","SWEPT_BODY",BODY,{"disambiguationData":[OSD([sQuery(id+"F0.wireOp",EDGE,"E1")])]}),"instanceName":"1"}),"instanceName":"1"}),"instanceName":"1"});
            var Q673;
            Q673=makeQuery(id+"F11.opPattern","COPY",BODY,{"derivedFrom":makeQuery(id+"F10.opPattern","COPY",BODY,{"derivedFrom":makeQuery(id+"F9.opPattern","COPY",BODY,{"derivedFrom":makeQuery(id+"F2.opPattern","COPY",BODY,{"derivedFrom":makeQuery(id+"F1.opRevolve","SWEPT_BODY",BODY,{"disambiguationData":[OSD([sQuery(id+"F0.wireOp",EDGE,"E1")])]}),"instanceName":"1"}),"instanceName":"1"}),"instanceName":"1"}),"instanceName":"1"});
            var Q674;
            Q674=makeQuery(id+"F11.opPattern","COPY",BODY,{"derivedFrom":makeQuery(id+"F10.opPattern","COPY",BODY,{"derivedFrom":makeQuery(id+"F9.opPattern","COPY",BODY,{"derivedFrom":makeQuery(id+"F3.opPattern","COPY",BODY,{"derivedFrom":makeQuery(id+"F2.opPattern","COPY",BODY,{"derivedFrom":makeQuery(id+"F1.opRevolve","SWEPT_BODY",BODY,{"disambiguationData":[OSD([sQuery(id+"F0.wireOp",EDGE,"E1")])]}),"instanceName":"1"}),"instanceName":"1"}),"instanceName":"1"}),"instanceName":"1"}),"instanceName":"1"});
            var Q675;
            Q675=makeQuery(id+"F11.opPattern","COPY",BODY,{"derivedFrom":makeQuery(id+"F10.opPattern","COPY",BODY,{"derivedFrom":makeQuery(id+"F9.opPattern","COPY",BODY,{"derivedFrom":makeQuery(id+"F4.opPattern","COPY",BODY,{"derivedFrom":makeQuery(id+"F1.opRevolve","SWEPT_BODY",BODY,{"disambiguationData":[OSD([sQuery(id+"F0.wireOp",EDGE,"E1")])]}),"instanceName":"1"}),"instanceName":"1"}),"instanceName":"1"}),"instanceName":"1"});
            var Q676;
            Q676=makeQuery(id+"F11.opPattern","COPY",BODY,{"derivedFrom":makeQuery(id+"F10.opPattern","COPY",BODY,{"derivedFrom":makeQuery(id+"F9.opPattern","COPY",BODY,{"derivedFrom":makeQuery(id+"F4.opPattern","COPY",BODY,{"derivedFrom":makeQuery(id+"F2.opPattern","COPY",BODY,{"derivedFrom":makeQuery(id+"F1.opRevolve","SWEPT_BODY",BODY,{"disambiguationData":[OSD([sQuery(id+"F0.wireOp",EDGE,"E1")])]}),"instanceName":"1"}),"instanceName":"1"}),"instanceName":"1"}),"instanceName":"1"}),"instanceName":"1"});
            var Q677;
            Q677=makeQuery(id+"F11.opPattern","COPY",BODY,{"derivedFrom":makeQuery(id+"F10.opPattern","COPY",BODY,{"derivedFrom":makeQuery(id+"F9.opPattern","COPY",BODY,{"derivedFrom":makeQuery(id+"F4.opPattern","COPY",BODY,{"derivedFrom":makeQuery(id+"F3.opPattern","COPY",BODY,{"derivedFrom":makeQuery(id+"F2.opPattern","COPY",BODY,{"derivedFrom":makeQuery(id+"F1.opRevolve","SWEPT_BODY",BODY,{"disambiguationData":[OSD([sQuery(id+"F0.wireOp",EDGE,"E1")])]}),"instanceName":"1"}),"instanceName":"1"}),"instanceName":"1"}),"instanceName":"1"}),"instanceName":"1"}),"instanceName":"1"});
            var Q678;
            Q678=makeQuery(id+"F11.opPattern","COPY",BODY,{"derivedFrom":makeQuery(id+"F10.opPattern","COPY",BODY,{"derivedFrom":makeQuery(id+"F9.opPattern","COPY",BODY,{"derivedFrom":makeQuery(id+"F5.opPattern","COPY",BODY,{"derivedFrom":makeQuery(id+"F1.opRevolve","SWEPT_BODY",BODY,{"disambiguationData":[OSD([sQuery(id+"F0.wireOp",EDGE,"E1")])]}),"instanceName":"1"}),"instanceName":"1"}),"instanceName":"1"}),"instanceName":"1"});
            var Q679;
            Q679=makeQuery(id+"F11.opPattern","COPY",BODY,{"derivedFrom":makeQuery(id+"F10.opPattern","COPY",BODY,{"derivedFrom":makeQuery(id+"F9.opPattern","COPY",BODY,{"derivedFrom":makeQuery(id+"F5.opPattern","COPY",BODY,{"derivedFrom":makeQuery(id+"F2.opPattern","COPY",BODY,{"derivedFrom":makeQuery(id+"F1.opRevolve","SWEPT_BODY",BODY,{"disambiguationData":[OSD([sQuery(id+"F0.wireOp",EDGE,"E1")])]}),"instanceName":"1"}),"instanceName":"1"}),"instanceName":"1"}),"instanceName":"1"}),"instanceName":"1"});
            var Q680;
            Q680=makeQuery(id+"F11.opPattern","COPY",BODY,{"derivedFrom":makeQuery(id+"F10.opPattern","COPY",BODY,{"derivedFrom":makeQuery(id+"F9.opPattern","COPY",BODY,{"derivedFrom":makeQuery(id+"F5.opPattern","COPY",BODY,{"derivedFrom":makeQuery(id+"F3.opPattern","COPY",BODY,{"derivedFrom":makeQuery(id+"F2.opPattern","COPY",BODY,{"derivedFrom":makeQuery(id+"F1.opRevolve","SWEPT_BODY",BODY,{"disambiguationData":[OSD([sQuery(id+"F0.wireOp",EDGE,"E1")])]}),"instanceName":"1"}),"instanceName":"1"}),"instanceName":"1"}),"instanceName":"1"}),"instanceName":"1"}),"instanceName":"1"});
            var Q681;
            Q681=makeQuery(id+"F11.opPattern","COPY",BODY,{"derivedFrom":makeQuery(id+"F10.opPattern","COPY",BODY,{"derivedFrom":makeQuery(id+"F9.opPattern","COPY",BODY,{"derivedFrom":makeQuery(id+"F5.opPattern","COPY",BODY,{"derivedFrom":makeQuery(id+"F4.opPattern","COPY",BODY,{"derivedFrom":makeQuery(id+"F1.opRevolve","SWEPT_BODY",BODY,{"disambiguationData":[OSD([sQuery(id+"F0.wireOp",EDGE,"E1")])]}),"instanceName":"1"}),"instanceName":"1"}),"instanceName":"1"}),"instanceName":"1"}),"instanceName":"1"});
            var Q682;
            Q682=makeQuery(id+"F11.opPattern","COPY",BODY,{"derivedFrom":makeQuery(id+"F10.opPattern","COPY",BODY,{"derivedFrom":makeQuery(id+"F9.opPattern","COPY",BODY,{"derivedFrom":makeQuery(id+"F5.opPattern","COPY",BODY,{"derivedFrom":makeQuery(id+"F4.opPattern","COPY",BODY,{"derivedFrom":makeQuery(id+"F2.opPattern","COPY",BODY,{"derivedFrom":makeQuery(id+"F1.opRevolve","SWEPT_BODY",BODY,{"disambiguationData":[OSD([sQuery(id+"F0.wireOp",EDGE,"E1")])]}),"instanceName":"1"}),"instanceName":"1"}),"instanceName":"1"}),"instanceName":"1"}),"instanceName":"1"}),"instanceName":"1"});
            var Q683;
            Q683=makeQuery(id+"F11.opPattern","COPY",BODY,{"derivedFrom":makeQuery(id+"F10.opPattern","COPY",BODY,{"derivedFrom":makeQuery(id+"F9.opPattern","COPY",BODY,{"derivedFrom":makeQuery(id+"F5.opPattern","COPY",BODY,{"derivedFrom":makeQuery(id+"F4.opPattern","COPY",BODY,{"derivedFrom":makeQuery(id+"F3.opPattern","COPY",BODY,{"derivedFrom":makeQuery(id+"F2.opPattern","COPY",BODY,{"derivedFrom":makeQuery(id+"F1.opRevolve","SWEPT_BODY",BODY,{"disambiguationData":[OSD([sQuery(id+"F0.wireOp",EDGE,"E1")])]}),"instanceName":"1"}),"instanceName":"1"}),"instanceName":"1"}),"instanceName":"1"}),"instanceName":"1"}),"instanceName":"1"}),"instanceName":"1"});
            var Q684;
            Q684=makeQuery(id+"F11.opPattern","COPY",BODY,{"derivedFrom":makeQuery(id+"F10.opPattern","COPY",BODY,{"derivedFrom":makeQuery(id+"F9.opPattern","COPY",BODY,{"derivedFrom":makeQuery(id+"F6.opPattern","COPY",BODY,{"derivedFrom":makeQuery(id+"F1.opRevolve","SWEPT_BODY",BODY,{"disambiguationData":[OSD([sQuery(id+"F0.wireOp",EDGE,"E1")])]}),"instanceName":"1"}),"instanceName":"1"}),"instanceName":"1"}),"instanceName":"1"});
            var Q685;
            Q685=makeQuery(id+"F11.opPattern","COPY",BODY,{"derivedFrom":makeQuery(id+"F10.opPattern","COPY",BODY,{"derivedFrom":makeQuery(id+"F9.opPattern","COPY",BODY,{"derivedFrom":makeQuery(id+"F6.opPattern","COPY",BODY,{"derivedFrom":makeQuery(id+"F2.opPattern","COPY",BODY,{"derivedFrom":makeQuery(id+"F1.opRevolve","SWEPT_BODY",BODY,{"disambiguationData":[OSD([sQuery(id+"F0.wireOp",EDGE,"E1")])]}),"instanceName":"1"}),"instanceName":"1"}),"instanceName":"1"}),"instanceName":"1"}),"instanceName":"1"});
            var Q686;
            Q686=makeQuery(id+"F11.opPattern","COPY",BODY,{"derivedFrom":makeQuery(id+"F10.opPattern","COPY",BODY,{"derivedFrom":makeQuery(id+"F9.opPattern","COPY",BODY,{"derivedFrom":makeQuery(id+"F6.opPattern","COPY",BODY,{"derivedFrom":makeQuery(id+"F3.opPattern","COPY",BODY,{"derivedFrom":makeQuery(id+"F2.opPattern","COPY",BODY,{"derivedFrom":makeQuery(id+"F1.opRevolve","SWEPT_BODY",BODY,{"disambiguationData":[OSD([sQuery(id+"F0.wireOp",EDGE,"E1")])]}),"instanceName":"1"}),"instanceName":"1"}),"instanceName":"1"}),"instanceName":"1"}),"instanceName":"1"}),"instanceName":"1"});
            var Q687;
            Q687=makeQuery(id+"F11.opPattern","COPY",BODY,{"derivedFrom":makeQuery(id+"F10.opPattern","COPY",BODY,{"derivedFrom":makeQuery(id+"F9.opPattern","COPY",BODY,{"derivedFrom":makeQuery(id+"F6.opPattern","COPY",BODY,{"derivedFrom":makeQuery(id+"F4.opPattern","COPY",BODY,{"derivedFrom":makeQuery(id+"F1.opRevolve","SWEPT_BODY",BODY,{"disambiguationData":[OSD([sQuery(id+"F0.wireOp",EDGE,"E1")])]}),"instanceName":"1"}),"instanceName":"1"}),"instanceName":"1"}),"instanceName":"1"}),"instanceName":"1"});
            var Q688;
            Q688=makeQuery(id+"F11.opPattern","COPY",BODY,{"derivedFrom":makeQuery(id+"F10.opPattern","COPY",BODY,{"derivedFrom":makeQuery(id+"F9.opPattern","COPY",BODY,{"derivedFrom":makeQuery(id+"F6.opPattern","COPY",BODY,{"derivedFrom":makeQuery(id+"F4.opPattern","COPY",BODY,{"derivedFrom":makeQuery(id+"F2.opPattern","COPY",BODY,{"derivedFrom":makeQuery(id+"F1.opRevolve","SWEPT_BODY",BODY,{"disambiguationData":[OSD([sQuery(id+"F0.wireOp",EDGE,"E1")])]}),"instanceName":"1"}),"instanceName":"1"}),"instanceName":"1"}),"instanceName":"1"}),"instanceName":"1"}),"instanceName":"1"});
            var Q689;
            Q689=makeQuery(id+"F11.opPattern","COPY",BODY,{"derivedFrom":makeQuery(id+"F10.opPattern","COPY",BODY,{"derivedFrom":makeQuery(id+"F9.opPattern","COPY",BODY,{"derivedFrom":makeQuery(id+"F6.opPattern","COPY",BODY,{"derivedFrom":makeQuery(id+"F4.opPattern","COPY",BODY,{"derivedFrom":makeQuery(id+"F3.opPattern","COPY",BODY,{"derivedFrom":makeQuery(id+"F2.opPattern","COPY",BODY,{"derivedFrom":makeQuery(id+"F1.opRevolve","SWEPT_BODY",BODY,{"disambiguationData":[OSD([sQuery(id+"F0.wireOp",EDGE,"E1")])]}),"instanceName":"1"}),"instanceName":"1"}),"instanceName":"1"}),"instanceName":"1"}),"instanceName":"1"}),"instanceName":"1"}),"instanceName":"1"});
            var Q690;
            Q690=makeQuery(id+"F11.opPattern","COPY",BODY,{"derivedFrom":makeQuery(id+"F10.opPattern","COPY",BODY,{"derivedFrom":makeQuery(id+"F9.opPattern","COPY",BODY,{"derivedFrom":makeQuery(id+"F6.opPattern","COPY",BODY,{"derivedFrom":makeQuery(id+"F5.opPattern","COPY",BODY,{"derivedFrom":makeQuery(id+"F1.opRevolve","SWEPT_BODY",BODY,{"disambiguationData":[OSD([sQuery(id+"F0.wireOp",EDGE,"E1")])]}),"instanceName":"1"}),"instanceName":"1"}),"instanceName":"1"}),"instanceName":"1"}),"instanceName":"1"});
            var Q691;
            Q691=makeQuery(id+"F11.opPattern","COPY",BODY,{"derivedFrom":makeQuery(id+"F10.opPattern","COPY",BODY,{"derivedFrom":makeQuery(id+"F9.opPattern","COPY",BODY,{"derivedFrom":makeQuery(id+"F6.opPattern","COPY",BODY,{"derivedFrom":makeQuery(id+"F5.opPattern","COPY",BODY,{"derivedFrom":makeQuery(id+"F2.opPattern","COPY",BODY,{"derivedFrom":makeQuery(id+"F1.opRevolve","SWEPT_BODY",BODY,{"disambiguationData":[OSD([sQuery(id+"F0.wireOp",EDGE,"E1")])]}),"instanceName":"1"}),"instanceName":"1"}),"instanceName":"1"}),"instanceName":"1"}),"instanceName":"1"}),"instanceName":"1"});
            var Q692;
            Q692=makeQuery(id+"F11.opPattern","COPY",BODY,{"derivedFrom":makeQuery(id+"F10.opPattern","COPY",BODY,{"derivedFrom":makeQuery(id+"F9.opPattern","COPY",BODY,{"derivedFrom":makeQuery(id+"F6.opPattern","COPY",BODY,{"derivedFrom":makeQuery(id+"F5.opPattern","COPY",BODY,{"derivedFrom":makeQuery(id+"F3.opPattern","COPY",BODY,{"derivedFrom":makeQuery(id+"F2.opPattern","COPY",BODY,{"derivedFrom":makeQuery(id+"F1.opRevolve","SWEPT_BODY",BODY,{"disambiguationData":[OSD([sQuery(id+"F0.wireOp",EDGE,"E1")])]}),"instanceName":"1"}),"instanceName":"1"}),"instanceName":"1"}),"instanceName":"1"}),"instanceName":"1"}),"instanceName":"1"}),"instanceName":"1"});
            var Q693;
            Q693=makeQuery(id+"F11.opPattern","COPY",BODY,{"derivedFrom":makeQuery(id+"F10.opPattern","COPY",BODY,{"derivedFrom":makeQuery(id+"F9.opPattern","COPY",BODY,{"derivedFrom":makeQuery(id+"F6.opPattern","COPY",BODY,{"derivedFrom":makeQuery(id+"F5.opPattern","COPY",BODY,{"derivedFrom":makeQuery(id+"F4.opPattern","COPY",BODY,{"derivedFrom":makeQuery(id+"F1.opRevolve","SWEPT_BODY",BODY,{"disambiguationData":[OSD([sQuery(id+"F0.wireOp",EDGE,"E1")])]}),"instanceName":"1"}),"instanceName":"1"}),"instanceName":"1"}),"instanceName":"1"}),"instanceName":"1"}),"instanceName":"1"});
            var Q694;
            Q694=makeQuery(id+"F11.opPattern","COPY",BODY,{"derivedFrom":makeQuery(id+"F10.opPattern","COPY",BODY,{"derivedFrom":makeQuery(id+"F9.opPattern","COPY",BODY,{"derivedFrom":makeQuery(id+"F6.opPattern","COPY",BODY,{"derivedFrom":makeQuery(id+"F5.opPattern","COPY",BODY,{"derivedFrom":makeQuery(id+"F4.opPattern","COPY",BODY,{"derivedFrom":makeQuery(id+"F2.opPattern","COPY",BODY,{"derivedFrom":makeQuery(id+"F1.opRevolve","SWEPT_BODY",BODY,{"disambiguationData":[OSD([sQuery(id+"F0.wireOp",EDGE,"E1")])]}),"instanceName":"1"}),"instanceName":"1"}),"instanceName":"1"}),"instanceName":"1"}),"instanceName":"1"}),"instanceName":"1"}),"instanceName":"1"});
            var Q695;
            Q695=makeQuery(id+"F11.opPattern","COPY",BODY,{"derivedFrom":makeQuery(id+"F10.opPattern","COPY",BODY,{"derivedFrom":makeQuery(id+"F9.opPattern","COPY",BODY,{"derivedFrom":makeQuery(id+"F6.opPattern","COPY",BODY,{"derivedFrom":makeQuery(id+"F5.opPattern","COPY",BODY,{"derivedFrom":makeQuery(id+"F4.opPattern","COPY",BODY,{"derivedFrom":makeQuery(id+"F3.opPattern","COPY",BODY,{"derivedFrom":makeQuery(id+"F2.opPattern","COPY",BODY,{"derivedFrom":makeQuery(id+"F1.opRevolve","SWEPT_BODY",BODY,{"disambiguationData":[OSD([sQuery(id+"F0.wireOp",EDGE,"E1")])]}),"instanceName":"1"}),"instanceName":"1"}),"instanceName":"1"}),"instanceName":"1"}),"instanceName":"1"}),"instanceName":"1"}),"instanceName":"1"}),"instanceName":"1"});
            var Q696;
            Q696=makeQuery(id+"F11.opPattern","COPY",BODY,{"derivedFrom":makeQuery(id+"F10.opPattern","COPY",BODY,{"derivedFrom":makeQuery(id+"F9.opPattern","COPY",BODY,{"derivedFrom":makeQuery(id+"F7.opPattern","COPY",BODY,{"derivedFrom":makeQuery(id+"F1.opRevolve","SWEPT_BODY",BODY,{"disambiguationData":[OSD([sQuery(id+"F0.wireOp",EDGE,"E1")])]}),"instanceName":"1"}),"instanceName":"1"}),"instanceName":"1"}),"instanceName":"1"});
            var Q697;
            Q697=makeQuery(id+"F11.opPattern","COPY",BODY,{"derivedFrom":makeQuery(id+"F10.opPattern","COPY",BODY,{"derivedFrom":makeQuery(id+"F9.opPattern","COPY",BODY,{"derivedFrom":makeQuery(id+"F7.opPattern","COPY",BODY,{"derivedFrom":makeQuery(id+"F2.opPattern","COPY",BODY,{"derivedFrom":makeQuery(id+"F1.opRevolve","SWEPT_BODY",BODY,{"disambiguationData":[OSD([sQuery(id+"F0.wireOp",EDGE,"E1")])]}),"instanceName":"1"}),"instanceName":"1"}),"instanceName":"1"}),"instanceName":"1"}),"instanceName":"1"});
            var Q698;
            Q698=makeQuery(id+"F11.opPattern","COPY",BODY,{"derivedFrom":makeQuery(id+"F10.opPattern","COPY",BODY,{"derivedFrom":makeQuery(id+"F9.opPattern","COPY",BODY,{"derivedFrom":makeQuery(id+"F7.opPattern","COPY",BODY,{"derivedFrom":makeQuery(id+"F3.opPattern","COPY",BODY,{"derivedFrom":makeQuery(id+"F2.opPattern","COPY",BODY,{"derivedFrom":makeQuery(id+"F1.opRevolve","SWEPT_BODY",BODY,{"disambiguationData":[OSD([sQuery(id+"F0.wireOp",EDGE,"E1")])]}),"instanceName":"1"}),"instanceName":"1"}),"instanceName":"1"}),"instanceName":"1"}),"instanceName":"1"}),"instanceName":"1"});
            var Q699;
            Q699=makeQuery(id+"F11.opPattern","COPY",BODY,{"derivedFrom":makeQuery(id+"F10.opPattern","COPY",BODY,{"derivedFrom":makeQuery(id+"F9.opPattern","COPY",BODY,{"derivedFrom":makeQuery(id+"F7.opPattern","COPY",BODY,{"derivedFrom":makeQuery(id+"F4.opPattern","COPY",BODY,{"derivedFrom":makeQuery(id+"F1.opRevolve","SWEPT_BODY",BODY,{"disambiguationData":[OSD([sQuery(id+"F0.wireOp",EDGE,"E1")])]}),"instanceName":"1"}),"instanceName":"1"}),"instanceName":"1"}),"instanceName":"1"}),"instanceName":"1"});
            var Q700;
            Q700=makeQuery(id+"F11.opPattern","COPY",BODY,{"derivedFrom":makeQuery(id+"F10.opPattern","COPY",BODY,{"derivedFrom":makeQuery(id+"F9.opPattern","COPY",BODY,{"derivedFrom":makeQuery(id+"F7.opPattern","COPY",BODY,{"derivedFrom":makeQuery(id+"F4.opPattern","COPY",BODY,{"derivedFrom":makeQuery(id+"F2.opPattern","COPY",BODY,{"derivedFrom":makeQuery(id+"F1.opRevolve","SWEPT_BODY",BODY,{"disambiguationData":[OSD([sQuery(id+"F0.wireOp",EDGE,"E1")])]}),"instanceName":"1"}),"instanceName":"1"}),"instanceName":"1"}),"instanceName":"1"}),"instanceName":"1"}),"instanceName":"1"});
            var Q701;
            Q701=makeQuery(id+"F11.opPattern","COPY",BODY,{"derivedFrom":makeQuery(id+"F10.opPattern","COPY",BODY,{"derivedFrom":makeQuery(id+"F9.opPattern","COPY",BODY,{"derivedFrom":makeQuery(id+"F7.opPattern","COPY",BODY,{"derivedFrom":makeQuery(id+"F4.opPattern","COPY",BODY,{"derivedFrom":makeQuery(id+"F3.opPattern","COPY",BODY,{"derivedFrom":makeQuery(id+"F2.opPattern","COPY",BODY,{"derivedFrom":makeQuery(id+"F1.opRevolve","SWEPT_BODY",BODY,{"disambiguationData":[OSD([sQuery(id+"F0.wireOp",EDGE,"E1")])]}),"instanceName":"1"}),"instanceName":"1"}),"instanceName":"1"}),"instanceName":"1"}),"instanceName":"1"}),"instanceName":"1"}),"instanceName":"1"});
            var Q702;
            Q702=makeQuery(id+"F11.opPattern","COPY",BODY,{"derivedFrom":makeQuery(id+"F10.opPattern","COPY",BODY,{"derivedFrom":makeQuery(id+"F9.opPattern","COPY",BODY,{"derivedFrom":makeQuery(id+"F7.opPattern","COPY",BODY,{"derivedFrom":makeQuery(id+"F5.opPattern","COPY",BODY,{"derivedFrom":makeQuery(id+"F1.opRevolve","SWEPT_BODY",BODY,{"disambiguationData":[OSD([sQuery(id+"F0.wireOp",EDGE,"E1")])]}),"instanceName":"1"}),"instanceName":"1"}),"instanceName":"1"}),"instanceName":"1"}),"instanceName":"1"});
            var Q703;
            Q703=makeQuery(id+"F11.opPattern","COPY",BODY,{"derivedFrom":makeQuery(id+"F10.opPattern","COPY",BODY,{"derivedFrom":makeQuery(id+"F9.opPattern","COPY",BODY,{"derivedFrom":makeQuery(id+"F7.opPattern","COPY",BODY,{"derivedFrom":makeQuery(id+"F5.opPattern","COPY",BODY,{"derivedFrom":makeQuery(id+"F2.opPattern","COPY",BODY,{"derivedFrom":makeQuery(id+"F1.opRevolve","SWEPT_BODY",BODY,{"disambiguationData":[OSD([sQuery(id+"F0.wireOp",EDGE,"E1")])]}),"instanceName":"1"}),"instanceName":"1"}),"instanceName":"1"}),"instanceName":"1"}),"instanceName":"1"}),"instanceName":"1"});
            var Q704;
            Q704=makeQuery(id+"F11.opPattern","COPY",BODY,{"derivedFrom":makeQuery(id+"F10.opPattern","COPY",BODY,{"derivedFrom":makeQuery(id+"F9.opPattern","COPY",BODY,{"derivedFrom":makeQuery(id+"F7.opPattern","COPY",BODY,{"derivedFrom":makeQuery(id+"F5.opPattern","COPY",BODY,{"derivedFrom":makeQuery(id+"F3.opPattern","COPY",BODY,{"derivedFrom":makeQuery(id+"F2.opPattern","COPY",BODY,{"derivedFrom":makeQuery(id+"F1.opRevolve","SWEPT_BODY",BODY,{"disambiguationData":[OSD([sQuery(id+"F0.wireOp",EDGE,"E1")])]}),"instanceName":"1"}),"instanceName":"1"}),"instanceName":"1"}),"instanceName":"1"}),"instanceName":"1"}),"instanceName":"1"}),"instanceName":"1"});
            var Q705;
            Q705=makeQuery(id+"F11.opPattern","COPY",BODY,{"derivedFrom":makeQuery(id+"F10.opPattern","COPY",BODY,{"derivedFrom":makeQuery(id+"F9.opPattern","COPY",BODY,{"derivedFrom":makeQuery(id+"F7.opPattern","COPY",BODY,{"derivedFrom":makeQuery(id+"F5.opPattern","COPY",BODY,{"derivedFrom":makeQuery(id+"F4.opPattern","COPY",BODY,{"derivedFrom":makeQuery(id+"F1.opRevolve","SWEPT_BODY",BODY,{"disambiguationData":[OSD([sQuery(id+"F0.wireOp",EDGE,"E1")])]}),"instanceName":"1"}),"instanceName":"1"}),"instanceName":"1"}),"instanceName":"1"}),"instanceName":"1"}),"instanceName":"1"});
            var Q706;
            Q706=makeQuery(id+"F11.opPattern","COPY",BODY,{"derivedFrom":makeQuery(id+"F10.opPattern","COPY",BODY,{"derivedFrom":makeQuery(id+"F9.opPattern","COPY",BODY,{"derivedFrom":makeQuery(id+"F7.opPattern","COPY",BODY,{"derivedFrom":makeQuery(id+"F5.opPattern","COPY",BODY,{"derivedFrom":makeQuery(id+"F4.opPattern","COPY",BODY,{"derivedFrom":makeQuery(id+"F2.opPattern","COPY",BODY,{"derivedFrom":makeQuery(id+"F1.opRevolve","SWEPT_BODY",BODY,{"disambiguationData":[OSD([sQuery(id+"F0.wireOp",EDGE,"E1")])]}),"instanceName":"1"}),"instanceName":"1"}),"instanceName":"1"}),"instanceName":"1"}),"instanceName":"1"}),"instanceName":"1"}),"instanceName":"1"});
            var Q707;
            Q707=makeQuery(id+"F11.opPattern","COPY",BODY,{"derivedFrom":makeQuery(id+"F10.opPattern","COPY",BODY,{"derivedFrom":makeQuery(id+"F9.opPattern","COPY",BODY,{"derivedFrom":makeQuery(id+"F7.opPattern","COPY",BODY,{"derivedFrom":makeQuery(id+"F5.opPattern","COPY",BODY,{"derivedFrom":makeQuery(id+"F4.opPattern","COPY",BODY,{"derivedFrom":makeQuery(id+"F3.opPattern","COPY",BODY,{"derivedFrom":makeQuery(id+"F2.opPattern","COPY",BODY,{"derivedFrom":makeQuery(id+"F1.opRevolve","SWEPT_BODY",BODY,{"disambiguationData":[OSD([sQuery(id+"F0.wireOp",EDGE,"E1")])]}),"instanceName":"1"}),"instanceName":"1"}),"instanceName":"1"}),"instanceName":"1"}),"instanceName":"1"}),"instanceName":"1"}),"instanceName":"1"}),"instanceName":"1"});
            var Q708;
            Q708=makeQuery(id+"F11.opPattern","COPY",BODY,{"derivedFrom":makeQuery(id+"F10.opPattern","COPY",BODY,{"derivedFrom":makeQuery(id+"F9.opPattern","COPY",BODY,{"derivedFrom":makeQuery(id+"F7.opPattern","COPY",BODY,{"derivedFrom":makeQuery(id+"F6.opPattern","COPY",BODY,{"derivedFrom":makeQuery(id+"F1.opRevolve","SWEPT_BODY",BODY,{"disambiguationData":[OSD([sQuery(id+"F0.wireOp",EDGE,"E1")])]}),"instanceName":"1"}),"instanceName":"1"}),"instanceName":"1"}),"instanceName":"1"}),"instanceName":"1"});
            var Q709;
            Q709=makeQuery(id+"F11.opPattern","COPY",BODY,{"derivedFrom":makeQuery(id+"F10.opPattern","COPY",BODY,{"derivedFrom":makeQuery(id+"F9.opPattern","COPY",BODY,{"derivedFrom":makeQuery(id+"F7.opPattern","COPY",BODY,{"derivedFrom":makeQuery(id+"F6.opPattern","COPY",BODY,{"derivedFrom":makeQuery(id+"F2.opPattern","COPY",BODY,{"derivedFrom":makeQuery(id+"F1.opRevolve","SWEPT_BODY",BODY,{"disambiguationData":[OSD([sQuery(id+"F0.wireOp",EDGE,"E1")])]}),"instanceName":"1"}),"instanceName":"1"}),"instanceName":"1"}),"instanceName":"1"}),"instanceName":"1"}),"instanceName":"1"});
            var Q710;
            Q710=makeQuery(id+"F11.opPattern","COPY",BODY,{"derivedFrom":makeQuery(id+"F10.opPattern","COPY",BODY,{"derivedFrom":makeQuery(id+"F9.opPattern","COPY",BODY,{"derivedFrom":makeQuery(id+"F7.opPattern","COPY",BODY,{"derivedFrom":makeQuery(id+"F6.opPattern","COPY",BODY,{"derivedFrom":makeQuery(id+"F3.opPattern","COPY",BODY,{"derivedFrom":makeQuery(id+"F2.opPattern","COPY",BODY,{"derivedFrom":makeQuery(id+"F1.opRevolve","SWEPT_BODY",BODY,{"disambiguationData":[OSD([sQuery(id+"F0.wireOp",EDGE,"E1")])]}),"instanceName":"1"}),"instanceName":"1"}),"instanceName":"1"}),"instanceName":"1"}),"instanceName":"1"}),"instanceName":"1"}),"instanceName":"1"});
            var Q711;
            Q711=makeQuery(id+"F11.opPattern","COPY",BODY,{"derivedFrom":makeQuery(id+"F10.opPattern","COPY",BODY,{"derivedFrom":makeQuery(id+"F9.opPattern","COPY",BODY,{"derivedFrom":makeQuery(id+"F7.opPattern","COPY",BODY,{"derivedFrom":makeQuery(id+"F6.opPattern","COPY",BODY,{"derivedFrom":makeQuery(id+"F4.opPattern","COPY",BODY,{"derivedFrom":makeQuery(id+"F1.opRevolve","SWEPT_BODY",BODY,{"disambiguationData":[OSD([sQuery(id+"F0.wireOp",EDGE,"E1")])]}),"instanceName":"1"}),"instanceName":"1"}),"instanceName":"1"}),"instanceName":"1"}),"instanceName":"1"}),"instanceName":"1"});
            var Q712;
            Q712=makeQuery(id+"F11.opPattern","COPY",BODY,{"derivedFrom":makeQuery(id+"F10.opPattern","COPY",BODY,{"derivedFrom":makeQuery(id+"F9.opPattern","COPY",BODY,{"derivedFrom":makeQuery(id+"F7.opPattern","COPY",BODY,{"derivedFrom":makeQuery(id+"F6.opPattern","COPY",BODY,{"derivedFrom":makeQuery(id+"F4.opPattern","COPY",BODY,{"derivedFrom":makeQuery(id+"F2.opPattern","COPY",BODY,{"derivedFrom":makeQuery(id+"F1.opRevolve","SWEPT_BODY",BODY,{"disambiguationData":[OSD([sQuery(id+"F0.wireOp",EDGE,"E1")])]}),"instanceName":"1"}),"instanceName":"1"}),"instanceName":"1"}),"instanceName":"1"}),"instanceName":"1"}),"instanceName":"1"}),"instanceName":"1"});
            var Q713;
            Q713=makeQuery(id+"F11.opPattern","COPY",BODY,{"derivedFrom":makeQuery(id+"F10.opPattern","COPY",BODY,{"derivedFrom":makeQuery(id+"F9.opPattern","COPY",BODY,{"derivedFrom":makeQuery(id+"F7.opPattern","COPY",BODY,{"derivedFrom":makeQuery(id+"F6.opPattern","COPY",BODY,{"derivedFrom":makeQuery(id+"F4.opPattern","COPY",BODY,{"derivedFrom":makeQuery(id+"F3.opPattern","COPY",BODY,{"derivedFrom":makeQuery(id+"F2.opPattern","COPY",BODY,{"derivedFrom":makeQuery(id+"F1.opRevolve","SWEPT_BODY",BODY,{"disambiguationData":[OSD([sQuery(id+"F0.wireOp",EDGE,"E1")])]}),"instanceName":"1"}),"instanceName":"1"}),"instanceName":"1"}),"instanceName":"1"}),"instanceName":"1"}),"instanceName":"1"}),"instanceName":"1"}),"instanceName":"1"});
            var Q714;
            Q714=makeQuery(id+"F11.opPattern","COPY",BODY,{"derivedFrom":makeQuery(id+"F10.opPattern","COPY",BODY,{"derivedFrom":makeQuery(id+"F9.opPattern","COPY",BODY,{"derivedFrom":makeQuery(id+"F7.opPattern","COPY",BODY,{"derivedFrom":makeQuery(id+"F6.opPattern","COPY",BODY,{"derivedFrom":makeQuery(id+"F5.opPattern","COPY",BODY,{"derivedFrom":makeQuery(id+"F1.opRevolve","SWEPT_BODY",BODY,{"disambiguationData":[OSD([sQuery(id+"F0.wireOp",EDGE,"E1")])]}),"instanceName":"1"}),"instanceName":"1"}),"instanceName":"1"}),"instanceName":"1"}),"instanceName":"1"}),"instanceName":"1"});
            var Q715;
            Q715=makeQuery(id+"F11.opPattern","COPY",BODY,{"derivedFrom":makeQuery(id+"F10.opPattern","COPY",BODY,{"derivedFrom":makeQuery(id+"F9.opPattern","COPY",BODY,{"derivedFrom":makeQuery(id+"F7.opPattern","COPY",BODY,{"derivedFrom":makeQuery(id+"F6.opPattern","COPY",BODY,{"derivedFrom":makeQuery(id+"F5.opPattern","COPY",BODY,{"derivedFrom":makeQuery(id+"F2.opPattern","COPY",BODY,{"derivedFrom":makeQuery(id+"F1.opRevolve","SWEPT_BODY",BODY,{"disambiguationData":[OSD([sQuery(id+"F0.wireOp",EDGE,"E1")])]}),"instanceName":"1"}),"instanceName":"1"}),"instanceName":"1"}),"instanceName":"1"}),"instanceName":"1"}),"instanceName":"1"}),"instanceName":"1"});
            var Q716;
            Q716=makeQuery(id+"F11.opPattern","COPY",BODY,{"derivedFrom":makeQuery(id+"F10.opPattern","COPY",BODY,{"derivedFrom":makeQuery(id+"F9.opPattern","COPY",BODY,{"derivedFrom":makeQuery(id+"F7.opPattern","COPY",BODY,{"derivedFrom":makeQuery(id+"F6.opPattern","COPY",BODY,{"derivedFrom":makeQuery(id+"F5.opPattern","COPY",BODY,{"derivedFrom":makeQuery(id+"F3.opPattern","COPY",BODY,{"derivedFrom":makeQuery(id+"F2.opPattern","COPY",BODY,{"derivedFrom":makeQuery(id+"F1.opRevolve","SWEPT_BODY",BODY,{"disambiguationData":[OSD([sQuery(id+"F0.wireOp",EDGE,"E1")])]}),"instanceName":"1"}),"instanceName":"1"}),"instanceName":"1"}),"instanceName":"1"}),"instanceName":"1"}),"instanceName":"1"}),"instanceName":"1"}),"instanceName":"1"});
            var Q717;
            Q717=makeQuery(id+"F11.opPattern","COPY",BODY,{"derivedFrom":makeQuery(id+"F10.opPattern","COPY",BODY,{"derivedFrom":makeQuery(id+"F9.opPattern","COPY",BODY,{"derivedFrom":makeQuery(id+"F7.opPattern","COPY",BODY,{"derivedFrom":makeQuery(id+"F6.opPattern","COPY",BODY,{"derivedFrom":makeQuery(id+"F5.opPattern","COPY",BODY,{"derivedFrom":makeQuery(id+"F4.opPattern","COPY",BODY,{"derivedFrom":makeQuery(id+"F1.opRevolve","SWEPT_BODY",BODY,{"disambiguationData":[OSD([sQuery(id+"F0.wireOp",EDGE,"E1")])]}),"instanceName":"1"}),"instanceName":"1"}),"instanceName":"1"}),"instanceName":"1"}),"instanceName":"1"}),"instanceName":"1"}),"instanceName":"1"});
            var Q718;
            Q718=makeQuery(id+"F11.opPattern","COPY",BODY,{"derivedFrom":makeQuery(id+"F10.opPattern","COPY",BODY,{"derivedFrom":makeQuery(id+"F9.opPattern","COPY",BODY,{"derivedFrom":makeQuery(id+"F7.opPattern","COPY",BODY,{"derivedFrom":makeQuery(id+"F6.opPattern","COPY",BODY,{"derivedFrom":makeQuery(id+"F5.opPattern","COPY",BODY,{"derivedFrom":makeQuery(id+"F4.opPattern","COPY",BODY,{"derivedFrom":makeQuery(id+"F2.opPattern","COPY",BODY,{"derivedFrom":makeQuery(id+"F1.opRevolve","SWEPT_BODY",BODY,{"disambiguationData":[OSD([sQuery(id+"F0.wireOp",EDGE,"E1")])]}),"instanceName":"1"}),"instanceName":"1"}),"instanceName":"1"}),"instanceName":"1"}),"instanceName":"1"}),"instanceName":"1"}),"instanceName":"1"}),"instanceName":"1"});
            var Q719;
            Q719=makeQuery(id+"F11.opPattern","COPY",BODY,{"derivedFrom":makeQuery(id+"F10.opPattern","COPY",BODY,{"derivedFrom":makeQuery(id+"F9.opPattern","COPY",BODY,{"derivedFrom":makeQuery(id+"F7.opPattern","COPY",BODY,{"derivedFrom":makeQuery(id+"F6.opPattern","COPY",BODY,{"derivedFrom":makeQuery(id+"F5.opPattern","COPY",BODY,{"derivedFrom":makeQuery(id+"F4.opPattern","COPY",BODY,{"derivedFrom":makeQuery(id+"F3.opPattern","COPY",BODY,{"derivedFrom":makeQuery(id+"F2.opPattern","COPY",BODY,{"derivedFrom":makeQuery(id+"F1.opRevolve","SWEPT_BODY",BODY,{"disambiguationData":[OSD([sQuery(id+"F0.wireOp",EDGE,"E1")])]}),"instanceName":"1"}),"instanceName":"1"}),"instanceName":"1"}),"instanceName":"1"}),"instanceName":"1"}),"instanceName":"1"}),"instanceName":"1"}),"instanceName":"1"}),"instanceName":"1"});
            var Q720;
            Q720=makeQuery(id+"F11.opPattern","COPY",BODY,{"derivedFrom":makeQuery(id+"F10.opPattern","COPY",BODY,{"derivedFrom":makeQuery(id+"F9.opPattern","COPY",BODY,{"derivedFrom":makeQuery(id+"F8.opPattern","COPY",BODY,{"derivedFrom":makeQuery(id+"F1.opRevolve","SWEPT_BODY",BODY,{"disambiguationData":[OSD([sQuery(id+"F0.wireOp",EDGE,"E1")])]}),"instanceName":"1"}),"instanceName":"1"}),"instanceName":"1"}),"instanceName":"1"});
            var Q721;
            Q721=makeQuery(id+"F11.opPattern","COPY",BODY,{"derivedFrom":makeQuery(id+"F10.opPattern","COPY",BODY,{"derivedFrom":makeQuery(id+"F9.opPattern","COPY",BODY,{"derivedFrom":makeQuery(id+"F8.opPattern","COPY",BODY,{"derivedFrom":makeQuery(id+"F2.opPattern","COPY",BODY,{"derivedFrom":makeQuery(id+"F1.opRevolve","SWEPT_BODY",BODY,{"disambiguationData":[OSD([sQuery(id+"F0.wireOp",EDGE,"E1")])]}),"instanceName":"1"}),"instanceName":"1"}),"instanceName":"1"}),"instanceName":"1"}),"instanceName":"1"});
            var Q722;
            Q722=makeQuery(id+"F11.opPattern","COPY",BODY,{"derivedFrom":makeQuery(id+"F10.opPattern","COPY",BODY,{"derivedFrom":makeQuery(id+"F9.opPattern","COPY",BODY,{"derivedFrom":makeQuery(id+"F8.opPattern","COPY",BODY,{"derivedFrom":makeQuery(id+"F3.opPattern","COPY",BODY,{"derivedFrom":makeQuery(id+"F2.opPattern","COPY",BODY,{"derivedFrom":makeQuery(id+"F1.opRevolve","SWEPT_BODY",BODY,{"disambiguationData":[OSD([sQuery(id+"F0.wireOp",EDGE,"E1")])]}),"instanceName":"1"}),"instanceName":"1"}),"instanceName":"1"}),"instanceName":"1"}),"instanceName":"1"}),"instanceName":"1"});
            var Q723;
            Q723=makeQuery(id+"F11.opPattern","COPY",BODY,{"derivedFrom":makeQuery(id+"F10.opPattern","COPY",BODY,{"derivedFrom":makeQuery(id+"F9.opPattern","COPY",BODY,{"derivedFrom":makeQuery(id+"F8.opPattern","COPY",BODY,{"derivedFrom":makeQuery(id+"F4.opPattern","COPY",BODY,{"derivedFrom":makeQuery(id+"F1.opRevolve","SWEPT_BODY",BODY,{"disambiguationData":[OSD([sQuery(id+"F0.wireOp",EDGE,"E1")])]}),"instanceName":"1"}),"instanceName":"1"}),"instanceName":"1"}),"instanceName":"1"}),"instanceName":"1"});
            var Q724;
            Q724=makeQuery(id+"F11.opPattern","COPY",BODY,{"derivedFrom":makeQuery(id+"F10.opPattern","COPY",BODY,{"derivedFrom":makeQuery(id+"F9.opPattern","COPY",BODY,{"derivedFrom":makeQuery(id+"F8.opPattern","COPY",BODY,{"derivedFrom":makeQuery(id+"F4.opPattern","COPY",BODY,{"derivedFrom":makeQuery(id+"F2.opPattern","COPY",BODY,{"derivedFrom":makeQuery(id+"F1.opRevolve","SWEPT_BODY",BODY,{"disambiguationData":[OSD([sQuery(id+"F0.wireOp",EDGE,"E1")])]}),"instanceName":"1"}),"instanceName":"1"}),"instanceName":"1"}),"instanceName":"1"}),"instanceName":"1"}),"instanceName":"1"});
            var Q725;
            Q725=makeQuery(id+"F11.opPattern","COPY",BODY,{"derivedFrom":makeQuery(id+"F10.opPattern","COPY",BODY,{"derivedFrom":makeQuery(id+"F9.opPattern","COPY",BODY,{"derivedFrom":makeQuery(id+"F8.opPattern","COPY",BODY,{"derivedFrom":makeQuery(id+"F4.opPattern","COPY",BODY,{"derivedFrom":makeQuery(id+"F3.opPattern","COPY",BODY,{"derivedFrom":makeQuery(id+"F2.opPattern","COPY",BODY,{"derivedFrom":makeQuery(id+"F1.opRevolve","SWEPT_BODY",BODY,{"disambiguationData":[OSD([sQuery(id+"F0.wireOp",EDGE,"E1")])]}),"instanceName":"1"}),"instanceName":"1"}),"instanceName":"1"}),"instanceName":"1"}),"instanceName":"1"}),"instanceName":"1"}),"instanceName":"1"});
            var Q726;
            Q726=makeQuery(id+"F11.opPattern","COPY",BODY,{"derivedFrom":makeQuery(id+"F10.opPattern","COPY",BODY,{"derivedFrom":makeQuery(id+"F9.opPattern","COPY",BODY,{"derivedFrom":makeQuery(id+"F8.opPattern","COPY",BODY,{"derivedFrom":makeQuery(id+"F5.opPattern","COPY",BODY,{"derivedFrom":makeQuery(id+"F1.opRevolve","SWEPT_BODY",BODY,{"disambiguationData":[OSD([sQuery(id+"F0.wireOp",EDGE,"E1")])]}),"instanceName":"1"}),"instanceName":"1"}),"instanceName":"1"}),"instanceName":"1"}),"instanceName":"1"});
            var Q727;
            Q727=makeQuery(id+"F11.opPattern","COPY",BODY,{"derivedFrom":makeQuery(id+"F10.opPattern","COPY",BODY,{"derivedFrom":makeQuery(id+"F9.opPattern","COPY",BODY,{"derivedFrom":makeQuery(id+"F8.opPattern","COPY",BODY,{"derivedFrom":makeQuery(id+"F5.opPattern","COPY",BODY,{"derivedFrom":makeQuery(id+"F2.opPattern","COPY",BODY,{"derivedFrom":makeQuery(id+"F1.opRevolve","SWEPT_BODY",BODY,{"disambiguationData":[OSD([sQuery(id+"F0.wireOp",EDGE,"E1")])]}),"instanceName":"1"}),"instanceName":"1"}),"instanceName":"1"}),"instanceName":"1"}),"instanceName":"1"}),"instanceName":"1"});
            var Q728;
            Q728=makeQuery(id+"F11.opPattern","COPY",BODY,{"derivedFrom":makeQuery(id+"F10.opPattern","COPY",BODY,{"derivedFrom":makeQuery(id+"F9.opPattern","COPY",BODY,{"derivedFrom":makeQuery(id+"F8.opPattern","COPY",BODY,{"derivedFrom":makeQuery(id+"F5.opPattern","COPY",BODY,{"derivedFrom":makeQuery(id+"F3.opPattern","COPY",BODY,{"derivedFrom":makeQuery(id+"F2.opPattern","COPY",BODY,{"derivedFrom":makeQuery(id+"F1.opRevolve","SWEPT_BODY",BODY,{"disambiguationData":[OSD([sQuery(id+"F0.wireOp",EDGE,"E1")])]}),"instanceName":"1"}),"instanceName":"1"}),"instanceName":"1"}),"instanceName":"1"}),"instanceName":"1"}),"instanceName":"1"}),"instanceName":"1"});
            var Q729;
            Q729=makeQuery(id+"F11.opPattern","COPY",BODY,{"derivedFrom":makeQuery(id+"F10.opPattern","COPY",BODY,{"derivedFrom":makeQuery(id+"F9.opPattern","COPY",BODY,{"derivedFrom":makeQuery(id+"F8.opPattern","COPY",BODY,{"derivedFrom":makeQuery(id+"F5.opPattern","COPY",BODY,{"derivedFrom":makeQuery(id+"F4.opPattern","COPY",BODY,{"derivedFrom":makeQuery(id+"F1.opRevolve","SWEPT_BODY",BODY,{"disambiguationData":[OSD([sQuery(id+"F0.wireOp",EDGE,"E1")])]}),"instanceName":"1"}),"instanceName":"1"}),"instanceName":"1"}),"instanceName":"1"}),"instanceName":"1"}),"instanceName":"1"});
            var Q730;
            Q730=makeQuery(id+"F11.opPattern","COPY",BODY,{"derivedFrom":makeQuery(id+"F10.opPattern","COPY",BODY,{"derivedFrom":makeQuery(id+"F9.opPattern","COPY",BODY,{"derivedFrom":makeQuery(id+"F8.opPattern","COPY",BODY,{"derivedFrom":makeQuery(id+"F5.opPattern","COPY",BODY,{"derivedFrom":makeQuery(id+"F4.opPattern","COPY",BODY,{"derivedFrom":makeQuery(id+"F2.opPattern","COPY",BODY,{"derivedFrom":makeQuery(id+"F1.opRevolve","SWEPT_BODY",BODY,{"disambiguationData":[OSD([sQuery(id+"F0.wireOp",EDGE,"E1")])]}),"instanceName":"1"}),"instanceName":"1"}),"instanceName":"1"}),"instanceName":"1"}),"instanceName":"1"}),"instanceName":"1"}),"instanceName":"1"});
            var Q731;
            Q731=makeQuery(id+"F11.opPattern","COPY",BODY,{"derivedFrom":makeQuery(id+"F10.opPattern","COPY",BODY,{"derivedFrom":makeQuery(id+"F9.opPattern","COPY",BODY,{"derivedFrom":makeQuery(id+"F8.opPattern","COPY",BODY,{"derivedFrom":makeQuery(id+"F5.opPattern","COPY",BODY,{"derivedFrom":makeQuery(id+"F4.opPattern","COPY",BODY,{"derivedFrom":makeQuery(id+"F3.opPattern","COPY",BODY,{"derivedFrom":makeQuery(id+"F2.opPattern","COPY",BODY,{"derivedFrom":makeQuery(id+"F1.opRevolve","SWEPT_BODY",BODY,{"disambiguationData":[OSD([sQuery(id+"F0.wireOp",EDGE,"E1")])]}),"instanceName":"1"}),"instanceName":"1"}),"instanceName":"1"}),"instanceName":"1"}),"instanceName":"1"}),"instanceName":"1"}),"instanceName":"1"}),"instanceName":"1"});
            var Q732;
            Q732=makeQuery(id+"F11.opPattern","COPY",BODY,{"derivedFrom":makeQuery(id+"F10.opPattern","COPY",BODY,{"derivedFrom":makeQuery(id+"F9.opPattern","COPY",BODY,{"derivedFrom":makeQuery(id+"F8.opPattern","COPY",BODY,{"derivedFrom":makeQuery(id+"F6.opPattern","COPY",BODY,{"derivedFrom":makeQuery(id+"F1.opRevolve","SWEPT_BODY",BODY,{"disambiguationData":[OSD([sQuery(id+"F0.wireOp",EDGE,"E1")])]}),"instanceName":"1"}),"instanceName":"1"}),"instanceName":"1"}),"instanceName":"1"}),"instanceName":"1"});
            var Q733;
            Q733=makeQuery(id+"F11.opPattern","COPY",BODY,{"derivedFrom":makeQuery(id+"F10.opPattern","COPY",BODY,{"derivedFrom":makeQuery(id+"F9.opPattern","COPY",BODY,{"derivedFrom":makeQuery(id+"F8.opPattern","COPY",BODY,{"derivedFrom":makeQuery(id+"F6.opPattern","COPY",BODY,{"derivedFrom":makeQuery(id+"F2.opPattern","COPY",BODY,{"derivedFrom":makeQuery(id+"F1.opRevolve","SWEPT_BODY",BODY,{"disambiguationData":[OSD([sQuery(id+"F0.wireOp",EDGE,"E1")])]}),"instanceName":"1"}),"instanceName":"1"}),"instanceName":"1"}),"instanceName":"1"}),"instanceName":"1"}),"instanceName":"1"});
            var Q734;
            Q734=makeQuery(id+"F11.opPattern","COPY",BODY,{"derivedFrom":makeQuery(id+"F10.opPattern","COPY",BODY,{"derivedFrom":makeQuery(id+"F9.opPattern","COPY",BODY,{"derivedFrom":makeQuery(id+"F8.opPattern","COPY",BODY,{"derivedFrom":makeQuery(id+"F6.opPattern","COPY",BODY,{"derivedFrom":makeQuery(id+"F3.opPattern","COPY",BODY,{"derivedFrom":makeQuery(id+"F2.opPattern","COPY",BODY,{"derivedFrom":makeQuery(id+"F1.opRevolve","SWEPT_BODY",BODY,{"disambiguationData":[OSD([sQuery(id+"F0.wireOp",EDGE,"E1")])]}),"instanceName":"1"}),"instanceName":"1"}),"instanceName":"1"}),"instanceName":"1"}),"instanceName":"1"}),"instanceName":"1"}),"instanceName":"1"});
            var Q735;
            Q735=makeQuery(id+"F11.opPattern","COPY",BODY,{"derivedFrom":makeQuery(id+"F10.opPattern","COPY",BODY,{"derivedFrom":makeQuery(id+"F9.opPattern","COPY",BODY,{"derivedFrom":makeQuery(id+"F8.opPattern","COPY",BODY,{"derivedFrom":makeQuery(id+"F6.opPattern","COPY",BODY,{"derivedFrom":makeQuery(id+"F4.opPattern","COPY",BODY,{"derivedFrom":makeQuery(id+"F1.opRevolve","SWEPT_BODY",BODY,{"disambiguationData":[OSD([sQuery(id+"F0.wireOp",EDGE,"E1")])]}),"instanceName":"1"}),"instanceName":"1"}),"instanceName":"1"}),"instanceName":"1"}),"instanceName":"1"}),"instanceName":"1"});
            var Q736;
            Q736=makeQuery(id+"F11.opPattern","COPY",BODY,{"derivedFrom":makeQuery(id+"F10.opPattern","COPY",BODY,{"derivedFrom":makeQuery(id+"F9.opPattern","COPY",BODY,{"derivedFrom":makeQuery(id+"F8.opPattern","COPY",BODY,{"derivedFrom":makeQuery(id+"F6.opPattern","COPY",BODY,{"derivedFrom":makeQuery(id+"F4.opPattern","COPY",BODY,{"derivedFrom":makeQuery(id+"F2.opPattern","COPY",BODY,{"derivedFrom":makeQuery(id+"F1.opRevolve","SWEPT_BODY",BODY,{"disambiguationData":[OSD([sQuery(id+"F0.wireOp",EDGE,"E1")])]}),"instanceName":"1"}),"instanceName":"1"}),"instanceName":"1"}),"instanceName":"1"}),"instanceName":"1"}),"instanceName":"1"}),"instanceName":"1"});
            var Q737;
            Q737=makeQuery(id+"F11.opPattern","COPY",BODY,{"derivedFrom":makeQuery(id+"F10.opPattern","COPY",BODY,{"derivedFrom":makeQuery(id+"F9.opPattern","COPY",BODY,{"derivedFrom":makeQuery(id+"F8.opPattern","COPY",BODY,{"derivedFrom":makeQuery(id+"F6.opPattern","COPY",BODY,{"derivedFrom":makeQuery(id+"F4.opPattern","COPY",BODY,{"derivedFrom":makeQuery(id+"F3.opPattern","COPY",BODY,{"derivedFrom":makeQuery(id+"F2.opPattern","COPY",BODY,{"derivedFrom":makeQuery(id+"F1.opRevolve","SWEPT_BODY",BODY,{"disambiguationData":[OSD([sQuery(id+"F0.wireOp",EDGE,"E1")])]}),"instanceName":"1"}),"instanceName":"1"}),"instanceName":"1"}),"instanceName":"1"}),"instanceName":"1"}),"instanceName":"1"}),"instanceName":"1"}),"instanceName":"1"});
            var Q738;
            Q738=makeQuery(id+"F11.opPattern","COPY",BODY,{"derivedFrom":makeQuery(id+"F10.opPattern","COPY",BODY,{"derivedFrom":makeQuery(id+"F9.opPattern","COPY",BODY,{"derivedFrom":makeQuery(id+"F8.opPattern","COPY",BODY,{"derivedFrom":makeQuery(id+"F6.opPattern","COPY",BODY,{"derivedFrom":makeQuery(id+"F5.opPattern","COPY",BODY,{"derivedFrom":makeQuery(id+"F1.opRevolve","SWEPT_BODY",BODY,{"disambiguationData":[OSD([sQuery(id+"F0.wireOp",EDGE,"E1")])]}),"instanceName":"1"}),"instanceName":"1"}),"instanceName":"1"}),"instanceName":"1"}),"instanceName":"1"}),"instanceName":"1"});
            var Q739;
            Q739=makeQuery(id+"F11.opPattern","COPY",BODY,{"derivedFrom":makeQuery(id+"F10.opPattern","COPY",BODY,{"derivedFrom":makeQuery(id+"F9.opPattern","COPY",BODY,{"derivedFrom":makeQuery(id+"F8.opPattern","COPY",BODY,{"derivedFrom":makeQuery(id+"F6.opPattern","COPY",BODY,{"derivedFrom":makeQuery(id+"F5.opPattern","COPY",BODY,{"derivedFrom":makeQuery(id+"F2.opPattern","COPY",BODY,{"derivedFrom":makeQuery(id+"F1.opRevolve","SWEPT_BODY",BODY,{"disambiguationData":[OSD([sQuery(id+"F0.wireOp",EDGE,"E1")])]}),"instanceName":"1"}),"instanceName":"1"}),"instanceName":"1"}),"instanceName":"1"}),"instanceName":"1"}),"instanceName":"1"}),"instanceName":"1"});
            var Q740;
            Q740=makeQuery(id+"F11.opPattern","COPY",BODY,{"derivedFrom":makeQuery(id+"F10.opPattern","COPY",BODY,{"derivedFrom":makeQuery(id+"F9.opPattern","COPY",BODY,{"derivedFrom":makeQuery(id+"F8.opPattern","COPY",BODY,{"derivedFrom":makeQuery(id+"F6.opPattern","COPY",BODY,{"derivedFrom":makeQuery(id+"F5.opPattern","COPY",BODY,{"derivedFrom":makeQuery(id+"F3.opPattern","COPY",BODY,{"derivedFrom":makeQuery(id+"F2.opPattern","COPY",BODY,{"derivedFrom":makeQuery(id+"F1.opRevolve","SWEPT_BODY",BODY,{"disambiguationData":[OSD([sQuery(id+"F0.wireOp",EDGE,"E1")])]}),"instanceName":"1"}),"instanceName":"1"}),"instanceName":"1"}),"instanceName":"1"}),"instanceName":"1"}),"instanceName":"1"}),"instanceName":"1"}),"instanceName":"1"});
            var Q741;
            Q741=makeQuery(id+"F11.opPattern","COPY",BODY,{"derivedFrom":makeQuery(id+"F10.opPattern","COPY",BODY,{"derivedFrom":makeQuery(id+"F9.opPattern","COPY",BODY,{"derivedFrom":makeQuery(id+"F8.opPattern","COPY",BODY,{"derivedFrom":makeQuery(id+"F6.opPattern","COPY",BODY,{"derivedFrom":makeQuery(id+"F5.opPattern","COPY",BODY,{"derivedFrom":makeQuery(id+"F4.opPattern","COPY",BODY,{"derivedFrom":makeQuery(id+"F1.opRevolve","SWEPT_BODY",BODY,{"disambiguationData":[OSD([sQuery(id+"F0.wireOp",EDGE,"E1")])]}),"instanceName":"1"}),"instanceName":"1"}),"instanceName":"1"}),"instanceName":"1"}),"instanceName":"1"}),"instanceName":"1"}),"instanceName":"1"});
            var Q742;
            Q742=makeQuery(id+"F11.opPattern","COPY",BODY,{"derivedFrom":makeQuery(id+"F10.opPattern","COPY",BODY,{"derivedFrom":makeQuery(id+"F9.opPattern","COPY",BODY,{"derivedFrom":makeQuery(id+"F8.opPattern","COPY",BODY,{"derivedFrom":makeQuery(id+"F6.opPattern","COPY",BODY,{"derivedFrom":makeQuery(id+"F5.opPattern","COPY",BODY,{"derivedFrom":makeQuery(id+"F4.opPattern","COPY",BODY,{"derivedFrom":makeQuery(id+"F2.opPattern","COPY",BODY,{"derivedFrom":makeQuery(id+"F1.opRevolve","SWEPT_BODY",BODY,{"disambiguationData":[OSD([sQuery(id+"F0.wireOp",EDGE,"E1")])]}),"instanceName":"1"}),"instanceName":"1"}),"instanceName":"1"}),"instanceName":"1"}),"instanceName":"1"}),"instanceName":"1"}),"instanceName":"1"}),"instanceName":"1"});
            var Q743;
            Q743=makeQuery(id+"F11.opPattern","COPY",BODY,{"derivedFrom":makeQuery(id+"F10.opPattern","COPY",BODY,{"derivedFrom":makeQuery(id+"F9.opPattern","COPY",BODY,{"derivedFrom":makeQuery(id+"F8.opPattern","COPY",BODY,{"derivedFrom":makeQuery(id+"F6.opPattern","COPY",BODY,{"derivedFrom":makeQuery(id+"F5.opPattern","COPY",BODY,{"derivedFrom":makeQuery(id+"F4.opPattern","COPY",BODY,{"derivedFrom":makeQuery(id+"F3.opPattern","COPY",BODY,{"derivedFrom":makeQuery(id+"F2.opPattern","COPY",BODY,{"derivedFrom":makeQuery(id+"F1.opRevolve","SWEPT_BODY",BODY,{"disambiguationData":[OSD([sQuery(id+"F0.wireOp",EDGE,"E1")])]}),"instanceName":"1"}),"instanceName":"1"}),"instanceName":"1"}),"instanceName":"1"}),"instanceName":"1"}),"instanceName":"1"}),"instanceName":"1"}),"instanceName":"1"}),"instanceName":"1"});
            var Q744;
            Q744=makeQuery(id+"F11.opPattern","COPY",BODY,{"derivedFrom":makeQuery(id+"F10.opPattern","COPY",BODY,{"derivedFrom":makeQuery(id+"F9.opPattern","COPY",BODY,{"derivedFrom":makeQuery(id+"F8.opPattern","COPY",BODY,{"derivedFrom":makeQuery(id+"F7.opPattern","COPY",BODY,{"derivedFrom":makeQuery(id+"F1.opRevolve","SWEPT_BODY",BODY,{"disambiguationData":[OSD([sQuery(id+"F0.wireOp",EDGE,"E1")])]}),"instanceName":"1"}),"instanceName":"1"}),"instanceName":"1"}),"instanceName":"1"}),"instanceName":"1"});
            var Q745;
            Q745=makeQuery(id+"F11.opPattern","COPY",BODY,{"derivedFrom":makeQuery(id+"F10.opPattern","COPY",BODY,{"derivedFrom":makeQuery(id+"F9.opPattern","COPY",BODY,{"derivedFrom":makeQuery(id+"F8.opPattern","COPY",BODY,{"derivedFrom":makeQuery(id+"F7.opPattern","COPY",BODY,{"derivedFrom":makeQuery(id+"F2.opPattern","COPY",BODY,{"derivedFrom":makeQuery(id+"F1.opRevolve","SWEPT_BODY",BODY,{"disambiguationData":[OSD([sQuery(id+"F0.wireOp",EDGE,"E1")])]}),"instanceName":"1"}),"instanceName":"1"}),"instanceName":"1"}),"instanceName":"1"}),"instanceName":"1"}),"instanceName":"1"});
            var Q746;
            Q746=makeQuery(id+"F11.opPattern","COPY",BODY,{"derivedFrom":makeQuery(id+"F10.opPattern","COPY",BODY,{"derivedFrom":makeQuery(id+"F9.opPattern","COPY",BODY,{"derivedFrom":makeQuery(id+"F8.opPattern","COPY",BODY,{"derivedFrom":makeQuery(id+"F7.opPattern","COPY",BODY,{"derivedFrom":makeQuery(id+"F3.opPattern","COPY",BODY,{"derivedFrom":makeQuery(id+"F2.opPattern","COPY",BODY,{"derivedFrom":makeQuery(id+"F1.opRevolve","SWEPT_BODY",BODY,{"disambiguationData":[OSD([sQuery(id+"F0.wireOp",EDGE,"E1")])]}),"instanceName":"1"}),"instanceName":"1"}),"instanceName":"1"}),"instanceName":"1"}),"instanceName":"1"}),"instanceName":"1"}),"instanceName":"1"});
            var Q747;
            Q747=makeQuery(id+"F11.opPattern","COPY",BODY,{"derivedFrom":makeQuery(id+"F10.opPattern","COPY",BODY,{"derivedFrom":makeQuery(id+"F9.opPattern","COPY",BODY,{"derivedFrom":makeQuery(id+"F8.opPattern","COPY",BODY,{"derivedFrom":makeQuery(id+"F7.opPattern","COPY",BODY,{"derivedFrom":makeQuery(id+"F4.opPattern","COPY",BODY,{"derivedFrom":makeQuery(id+"F1.opRevolve","SWEPT_BODY",BODY,{"disambiguationData":[OSD([sQuery(id+"F0.wireOp",EDGE,"E1")])]}),"instanceName":"1"}),"instanceName":"1"}),"instanceName":"1"}),"instanceName":"1"}),"instanceName":"1"}),"instanceName":"1"});
            var Q748;
            Q748=makeQuery(id+"F11.opPattern","COPY",BODY,{"derivedFrom":makeQuery(id+"F10.opPattern","COPY",BODY,{"derivedFrom":makeQuery(id+"F9.opPattern","COPY",BODY,{"derivedFrom":makeQuery(id+"F8.opPattern","COPY",BODY,{"derivedFrom":makeQuery(id+"F7.opPattern","COPY",BODY,{"derivedFrom":makeQuery(id+"F4.opPattern","COPY",BODY,{"derivedFrom":makeQuery(id+"F2.opPattern","COPY",BODY,{"derivedFrom":makeQuery(id+"F1.opRevolve","SWEPT_BODY",BODY,{"disambiguationData":[OSD([sQuery(id+"F0.wireOp",EDGE,"E1")])]}),"instanceName":"1"}),"instanceName":"1"}),"instanceName":"1"}),"instanceName":"1"}),"instanceName":"1"}),"instanceName":"1"}),"instanceName":"1"});
            var Q749;
            Q749=makeQuery(id+"F11.opPattern","COPY",BODY,{"derivedFrom":makeQuery(id+"F10.opPattern","COPY",BODY,{"derivedFrom":makeQuery(id+"F9.opPattern","COPY",BODY,{"derivedFrom":makeQuery(id+"F8.opPattern","COPY",BODY,{"derivedFrom":makeQuery(id+"F7.opPattern","COPY",BODY,{"derivedFrom":makeQuery(id+"F4.opPattern","COPY",BODY,{"derivedFrom":makeQuery(id+"F3.opPattern","COPY",BODY,{"derivedFrom":makeQuery(id+"F2.opPattern","COPY",BODY,{"derivedFrom":makeQuery(id+"F1.opRevolve","SWEPT_BODY",BODY,{"disambiguationData":[OSD([sQuery(id+"F0.wireOp",EDGE,"E1")])]}),"instanceName":"1"}),"instanceName":"1"}),"instanceName":"1"}),"instanceName":"1"}),"instanceName":"1"}),"instanceName":"1"}),"instanceName":"1"}),"instanceName":"1"});
            var Q750;
            Q750=makeQuery(id+"F11.opPattern","COPY",BODY,{"derivedFrom":makeQuery(id+"F10.opPattern","COPY",BODY,{"derivedFrom":makeQuery(id+"F9.opPattern","COPY",BODY,{"derivedFrom":makeQuery(id+"F8.opPattern","COPY",BODY,{"derivedFrom":makeQuery(id+"F7.opPattern","COPY",BODY,{"derivedFrom":makeQuery(id+"F5.opPattern","COPY",BODY,{"derivedFrom":makeQuery(id+"F1.opRevolve","SWEPT_BODY",BODY,{"disambiguationData":[OSD([sQuery(id+"F0.wireOp",EDGE,"E1")])]}),"instanceName":"1"}),"instanceName":"1"}),"instanceName":"1"}),"instanceName":"1"}),"instanceName":"1"}),"instanceName":"1"});
            var Q751;
            Q751=makeQuery(id+"F11.opPattern","COPY",BODY,{"derivedFrom":makeQuery(id+"F10.opPattern","COPY",BODY,{"derivedFrom":makeQuery(id+"F9.opPattern","COPY",BODY,{"derivedFrom":makeQuery(id+"F8.opPattern","COPY",BODY,{"derivedFrom":makeQuery(id+"F7.opPattern","COPY",BODY,{"derivedFrom":makeQuery(id+"F5.opPattern","COPY",BODY,{"derivedFrom":makeQuery(id+"F2.opPattern","COPY",BODY,{"derivedFrom":makeQuery(id+"F1.opRevolve","SWEPT_BODY",BODY,{"disambiguationData":[OSD([sQuery(id+"F0.wireOp",EDGE,"E1")])]}),"instanceName":"1"}),"instanceName":"1"}),"instanceName":"1"}),"instanceName":"1"}),"instanceName":"1"}),"instanceName":"1"}),"instanceName":"1"});
            var Q752;
            Q752=makeQuery(id+"F11.opPattern","COPY",BODY,{"derivedFrom":makeQuery(id+"F10.opPattern","COPY",BODY,{"derivedFrom":makeQuery(id+"F9.opPattern","COPY",BODY,{"derivedFrom":makeQuery(id+"F8.opPattern","COPY",BODY,{"derivedFrom":makeQuery(id+"F7.opPattern","COPY",BODY,{"derivedFrom":makeQuery(id+"F5.opPattern","COPY",BODY,{"derivedFrom":makeQuery(id+"F3.opPattern","COPY",BODY,{"derivedFrom":makeQuery(id+"F2.opPattern","COPY",BODY,{"derivedFrom":makeQuery(id+"F1.opRevolve","SWEPT_BODY",BODY,{"disambiguationData":[OSD([sQuery(id+"F0.wireOp",EDGE,"E1")])]}),"instanceName":"1"}),"instanceName":"1"}),"instanceName":"1"}),"instanceName":"1"}),"instanceName":"1"}),"instanceName":"1"}),"instanceName":"1"}),"instanceName":"1"});
            var Q753;
            Q753=makeQuery(id+"F11.opPattern","COPY",BODY,{"derivedFrom":makeQuery(id+"F10.opPattern","COPY",BODY,{"derivedFrom":makeQuery(id+"F9.opPattern","COPY",BODY,{"derivedFrom":makeQuery(id+"F8.opPattern","COPY",BODY,{"derivedFrom":makeQuery(id+"F7.opPattern","COPY",BODY,{"derivedFrom":makeQuery(id+"F5.opPattern","COPY",BODY,{"derivedFrom":makeQuery(id+"F4.opPattern","COPY",BODY,{"derivedFrom":makeQuery(id+"F1.opRevolve","SWEPT_BODY",BODY,{"disambiguationData":[OSD([sQuery(id+"F0.wireOp",EDGE,"E1")])]}),"instanceName":"1"}),"instanceName":"1"}),"instanceName":"1"}),"instanceName":"1"}),"instanceName":"1"}),"instanceName":"1"}),"instanceName":"1"});
            var Q754;
            Q754=makeQuery(id+"F11.opPattern","COPY",BODY,{"derivedFrom":makeQuery(id+"F10.opPattern","COPY",BODY,{"derivedFrom":makeQuery(id+"F9.opPattern","COPY",BODY,{"derivedFrom":makeQuery(id+"F8.opPattern","COPY",BODY,{"derivedFrom":makeQuery(id+"F7.opPattern","COPY",BODY,{"derivedFrom":makeQuery(id+"F5.opPattern","COPY",BODY,{"derivedFrom":makeQuery(id+"F4.opPattern","COPY",BODY,{"derivedFrom":makeQuery(id+"F2.opPattern","COPY",BODY,{"derivedFrom":makeQuery(id+"F1.opRevolve","SWEPT_BODY",BODY,{"disambiguationData":[OSD([sQuery(id+"F0.wireOp",EDGE,"E1")])]}),"instanceName":"1"}),"instanceName":"1"}),"instanceName":"1"}),"instanceName":"1"}),"instanceName":"1"}),"instanceName":"1"}),"instanceName":"1"}),"instanceName":"1"});
            var Q755;
            Q755=makeQuery(id+"F11.opPattern","COPY",BODY,{"derivedFrom":makeQuery(id+"F10.opPattern","COPY",BODY,{"derivedFrom":makeQuery(id+"F9.opPattern","COPY",BODY,{"derivedFrom":makeQuery(id+"F8.opPattern","COPY",BODY,{"derivedFrom":makeQuery(id+"F7.opPattern","COPY",BODY,{"derivedFrom":makeQuery(id+"F5.opPattern","COPY",BODY,{"derivedFrom":makeQuery(id+"F4.opPattern","COPY",BODY,{"derivedFrom":makeQuery(id+"F3.opPattern","COPY",BODY,{"derivedFrom":makeQuery(id+"F2.opPattern","COPY",BODY,{"derivedFrom":makeQuery(id+"F1.opRevolve","SWEPT_BODY",BODY,{"disambiguationData":[OSD([sQuery(id+"F0.wireOp",EDGE,"E1")])]}),"instanceName":"1"}),"instanceName":"1"}),"instanceName":"1"}),"instanceName":"1"}),"instanceName":"1"}),"instanceName":"1"}),"instanceName":"1"}),"instanceName":"1"}),"instanceName":"1"});
            var Q756;
            Q756=makeQuery(id+"F11.opPattern","COPY",BODY,{"derivedFrom":makeQuery(id+"F10.opPattern","COPY",BODY,{"derivedFrom":makeQuery(id+"F9.opPattern","COPY",BODY,{"derivedFrom":makeQuery(id+"F8.opPattern","COPY",BODY,{"derivedFrom":makeQuery(id+"F7.opPattern","COPY",BODY,{"derivedFrom":makeQuery(id+"F6.opPattern","COPY",BODY,{"derivedFrom":makeQuery(id+"F1.opRevolve","SWEPT_BODY",BODY,{"disambiguationData":[OSD([sQuery(id+"F0.wireOp",EDGE,"E1")])]}),"instanceName":"1"}),"instanceName":"1"}),"instanceName":"1"}),"instanceName":"1"}),"instanceName":"1"}),"instanceName":"1"});
            var Q757;
            Q757=makeQuery(id+"F11.opPattern","COPY",BODY,{"derivedFrom":makeQuery(id+"F10.opPattern","COPY",BODY,{"derivedFrom":makeQuery(id+"F9.opPattern","COPY",BODY,{"derivedFrom":makeQuery(id+"F8.opPattern","COPY",BODY,{"derivedFrom":makeQuery(id+"F7.opPattern","COPY",BODY,{"derivedFrom":makeQuery(id+"F6.opPattern","COPY",BODY,{"derivedFrom":makeQuery(id+"F2.opPattern","COPY",BODY,{"derivedFrom":makeQuery(id+"F1.opRevolve","SWEPT_BODY",BODY,{"disambiguationData":[OSD([sQuery(id+"F0.wireOp",EDGE,"E1")])]}),"instanceName":"1"}),"instanceName":"1"}),"instanceName":"1"}),"instanceName":"1"}),"instanceName":"1"}),"instanceName":"1"}),"instanceName":"1"});
            var Q758;
            Q758=makeQuery(id+"F11.opPattern","COPY",BODY,{"derivedFrom":makeQuery(id+"F10.opPattern","COPY",BODY,{"derivedFrom":makeQuery(id+"F9.opPattern","COPY",BODY,{"derivedFrom":makeQuery(id+"F8.opPattern","COPY",BODY,{"derivedFrom":makeQuery(id+"F7.opPattern","COPY",BODY,{"derivedFrom":makeQuery(id+"F6.opPattern","COPY",BODY,{"derivedFrom":makeQuery(id+"F3.opPattern","COPY",BODY,{"derivedFrom":makeQuery(id+"F2.opPattern","COPY",BODY,{"derivedFrom":makeQuery(id+"F1.opRevolve","SWEPT_BODY",BODY,{"disambiguationData":[OSD([sQuery(id+"F0.wireOp",EDGE,"E1")])]}),"instanceName":"1"}),"instanceName":"1"}),"instanceName":"1"}),"instanceName":"1"}),"instanceName":"1"}),"instanceName":"1"}),"instanceName":"1"}),"instanceName":"1"});
            var Q759;
            Q759=makeQuery(id+"F11.opPattern","COPY",BODY,{"derivedFrom":makeQuery(id+"F10.opPattern","COPY",BODY,{"derivedFrom":makeQuery(id+"F9.opPattern","COPY",BODY,{"derivedFrom":makeQuery(id+"F8.opPattern","COPY",BODY,{"derivedFrom":makeQuery(id+"F7.opPattern","COPY",BODY,{"derivedFrom":makeQuery(id+"F6.opPattern","COPY",BODY,{"derivedFrom":makeQuery(id+"F4.opPattern","COPY",BODY,{"derivedFrom":makeQuery(id+"F1.opRevolve","SWEPT_BODY",BODY,{"disambiguationData":[OSD([sQuery(id+"F0.wireOp",EDGE,"E1")])]}),"instanceName":"1"}),"instanceName":"1"}),"instanceName":"1"}),"instanceName":"1"}),"instanceName":"1"}),"instanceName":"1"}),"instanceName":"1"});
            var Q760;
            Q760=makeQuery(id+"F11.opPattern","COPY",BODY,{"derivedFrom":makeQuery(id+"F10.opPattern","COPY",BODY,{"derivedFrom":makeQuery(id+"F9.opPattern","COPY",BODY,{"derivedFrom":makeQuery(id+"F8.opPattern","COPY",BODY,{"derivedFrom":makeQuery(id+"F7.opPattern","COPY",BODY,{"derivedFrom":makeQuery(id+"F6.opPattern","COPY",BODY,{"derivedFrom":makeQuery(id+"F4.opPattern","COPY",BODY,{"derivedFrom":makeQuery(id+"F2.opPattern","COPY",BODY,{"derivedFrom":makeQuery(id+"F1.opRevolve","SWEPT_BODY",BODY,{"disambiguationData":[OSD([sQuery(id+"F0.wireOp",EDGE,"E1")])]}),"instanceName":"1"}),"instanceName":"1"}),"instanceName":"1"}),"instanceName":"1"}),"instanceName":"1"}),"instanceName":"1"}),"instanceName":"1"}),"instanceName":"1"});
            var Q761;
            Q761=makeQuery(id+"F11.opPattern","COPY",BODY,{"derivedFrom":makeQuery(id+"F10.opPattern","COPY",BODY,{"derivedFrom":makeQuery(id+"F9.opPattern","COPY",BODY,{"derivedFrom":makeQuery(id+"F8.opPattern","COPY",BODY,{"derivedFrom":makeQuery(id+"F7.opPattern","COPY",BODY,{"derivedFrom":makeQuery(id+"F6.opPattern","COPY",BODY,{"derivedFrom":makeQuery(id+"F4.opPattern","COPY",BODY,{"derivedFrom":makeQuery(id+"F3.opPattern","COPY",BODY,{"derivedFrom":makeQuery(id+"F2.opPattern","COPY",BODY,{"derivedFrom":makeQuery(id+"F1.opRevolve","SWEPT_BODY",BODY,{"disambiguationData":[OSD([sQuery(id+"F0.wireOp",EDGE,"E1")])]}),"instanceName":"1"}),"instanceName":"1"}),"instanceName":"1"}),"instanceName":"1"}),"instanceName":"1"}),"instanceName":"1"}),"instanceName":"1"}),"instanceName":"1"}),"instanceName":"1"});
            var Q762;
            Q762=makeQuery(id+"F11.opPattern","COPY",BODY,{"derivedFrom":makeQuery(id+"F10.opPattern","COPY",BODY,{"derivedFrom":makeQuery(id+"F9.opPattern","COPY",BODY,{"derivedFrom":makeQuery(id+"F8.opPattern","COPY",BODY,{"derivedFrom":makeQuery(id+"F7.opPattern","COPY",BODY,{"derivedFrom":makeQuery(id+"F6.opPattern","COPY",BODY,{"derivedFrom":makeQuery(id+"F5.opPattern","COPY",BODY,{"derivedFrom":makeQuery(id+"F1.opRevolve","SWEPT_BODY",BODY,{"disambiguationData":[OSD([sQuery(id+"F0.wireOp",EDGE,"E1")])]}),"instanceName":"1"}),"instanceName":"1"}),"instanceName":"1"}),"instanceName":"1"}),"instanceName":"1"}),"instanceName":"1"}),"instanceName":"1"});
            var Q763;
            Q763=makeQuery(id+"F11.opPattern","COPY",BODY,{"derivedFrom":makeQuery(id+"F10.opPattern","COPY",BODY,{"derivedFrom":makeQuery(id+"F9.opPattern","COPY",BODY,{"derivedFrom":makeQuery(id+"F8.opPattern","COPY",BODY,{"derivedFrom":makeQuery(id+"F7.opPattern","COPY",BODY,{"derivedFrom":makeQuery(id+"F6.opPattern","COPY",BODY,{"derivedFrom":makeQuery(id+"F5.opPattern","COPY",BODY,{"derivedFrom":makeQuery(id+"F2.opPattern","COPY",BODY,{"derivedFrom":makeQuery(id+"F1.opRevolve","SWEPT_BODY",BODY,{"disambiguationData":[OSD([sQuery(id+"F0.wireOp",EDGE,"E1")])]}),"instanceName":"1"}),"instanceName":"1"}),"instanceName":"1"}),"instanceName":"1"}),"instanceName":"1"}),"instanceName":"1"}),"instanceName":"1"}),"instanceName":"1"});
            var Q764;
            Q764=makeQuery(id+"F11.opPattern","COPY",BODY,{"derivedFrom":makeQuery(id+"F10.opPattern","COPY",BODY,{"derivedFrom":makeQuery(id+"F9.opPattern","COPY",BODY,{"derivedFrom":makeQuery(id+"F8.opPattern","COPY",BODY,{"derivedFrom":makeQuery(id+"F7.opPattern","COPY",BODY,{"derivedFrom":makeQuery(id+"F6.opPattern","COPY",BODY,{"derivedFrom":makeQuery(id+"F5.opPattern","COPY",BODY,{"derivedFrom":makeQuery(id+"F3.opPattern","COPY",BODY,{"derivedFrom":makeQuery(id+"F2.opPattern","COPY",BODY,{"derivedFrom":makeQuery(id+"F1.opRevolve","SWEPT_BODY",BODY,{"disambiguationData":[OSD([sQuery(id+"F0.wireOp",EDGE,"E1")])]}),"instanceName":"1"}),"instanceName":"1"}),"instanceName":"1"}),"instanceName":"1"}),"instanceName":"1"}),"instanceName":"1"}),"instanceName":"1"}),"instanceName":"1"}),"instanceName":"1"});
            var Q765;
            Q765=makeQuery(id+"F11.opPattern","COPY",BODY,{"derivedFrom":makeQuery(id+"F10.opPattern","COPY",BODY,{"derivedFrom":makeQuery(id+"F9.opPattern","COPY",BODY,{"derivedFrom":makeQuery(id+"F8.opPattern","COPY",BODY,{"derivedFrom":makeQuery(id+"F7.opPattern","COPY",BODY,{"derivedFrom":makeQuery(id+"F6.opPattern","COPY",BODY,{"derivedFrom":makeQuery(id+"F5.opPattern","COPY",BODY,{"derivedFrom":makeQuery(id+"F4.opPattern","COPY",BODY,{"derivedFrom":makeQuery(id+"F1.opRevolve","SWEPT_BODY",BODY,{"disambiguationData":[OSD([sQuery(id+"F0.wireOp",EDGE,"E1")])]}),"instanceName":"1"}),"instanceName":"1"}),"instanceName":"1"}),"instanceName":"1"}),"instanceName":"1"}),"instanceName":"1"}),"instanceName":"1"}),"instanceName":"1"});
            var Q766;
            Q766=makeQuery(id+"F11.opPattern","COPY",BODY,{"derivedFrom":makeQuery(id+"F10.opPattern","COPY",BODY,{"derivedFrom":makeQuery(id+"F9.opPattern","COPY",BODY,{"derivedFrom":makeQuery(id+"F8.opPattern","COPY",BODY,{"derivedFrom":makeQuery(id+"F7.opPattern","COPY",BODY,{"derivedFrom":makeQuery(id+"F6.opPattern","COPY",BODY,{"derivedFrom":makeQuery(id+"F5.opPattern","COPY",BODY,{"derivedFrom":makeQuery(id+"F4.opPattern","COPY",BODY,{"derivedFrom":makeQuery(id+"F2.opPattern","COPY",BODY,{"derivedFrom":makeQuery(id+"F1.opRevolve","SWEPT_BODY",BODY,{"disambiguationData":[OSD([sQuery(id+"F0.wireOp",EDGE,"E1")])]}),"instanceName":"1"}),"instanceName":"1"}),"instanceName":"1"}),"instanceName":"1"}),"instanceName":"1"}),"instanceName":"1"}),"instanceName":"1"}),"instanceName":"1"}),"instanceName":"1"});
            var Q767;
            Q767=makeQuery(id+"F11.opPattern","COPY",BODY,{"derivedFrom":makeQuery(id+"F10.opPattern","COPY",BODY,{"derivedFrom":makeQuery(id+"F9.opPattern","COPY",BODY,{"derivedFrom":makeQuery(id+"F8.opPattern","COPY",BODY,{"derivedFrom":makeQuery(id+"F7.opPattern","COPY",BODY,{"derivedFrom":makeQuery(id+"F6.opPattern","COPY",BODY,{"derivedFrom":makeQuery(id+"F5.opPattern","COPY",BODY,{"derivedFrom":makeQuery(id+"F4.opPattern","COPY",BODY,{"derivedFrom":makeQuery(id+"F3.opPattern","COPY",BODY,{"derivedFrom":makeQuery(id+"F2.opPattern","COPY",BODY,{"derivedFrom":makeQuery(id+"F1.opRevolve","SWEPT_BODY",BODY,{"disambiguationData":[OSD([sQuery(id+"F0.wireOp",EDGE,"E1")])]}),"instanceName":"1"}),"instanceName":"1"}),"instanceName":"1"}),"instanceName":"1"}),"instanceName":"1"}),"instanceName":"1"}),"instanceName":"1"}),"instanceName":"1"}),"instanceName":"1"}),"instanceName":"1"});
            var Q768;
            Q768=makeQuery(id+"F12.opPattern","COPY",BODY,{"derivedFrom":makeQuery(id+"F1.opRevolve","SWEPT_BODY",BODY,{"disambiguationData":[OSD([sQuery(id+"F0.wireOp",EDGE,"E1")])]}),"instanceName":"1"});
            var Q769;
            Q769=makeQuery(id+"F12.opPattern","COPY",BODY,{"derivedFrom":makeQuery(id+"F2.opPattern","COPY",BODY,{"derivedFrom":makeQuery(id+"F1.opRevolve","SWEPT_BODY",BODY,{"disambiguationData":[OSD([sQuery(id+"F0.wireOp",EDGE,"E1")])]}),"instanceName":"1"}),"instanceName":"1"});
            var Q770;
            Q770=makeQuery(id+"F12.opPattern","COPY",BODY,{"derivedFrom":makeQuery(id+"F3.opPattern","COPY",BODY,{"derivedFrom":makeQuery(id+"F2.opPattern","COPY",BODY,{"derivedFrom":makeQuery(id+"F1.opRevolve","SWEPT_BODY",BODY,{"disambiguationData":[OSD([sQuery(id+"F0.wireOp",EDGE,"E1")])]}),"instanceName":"1"}),"instanceName":"1"}),"instanceName":"1"});
            var Q771;
            Q771=makeQuery(id+"F12.opPattern","COPY",BODY,{"derivedFrom":makeQuery(id+"F4.opPattern","COPY",BODY,{"derivedFrom":makeQuery(id+"F1.opRevolve","SWEPT_BODY",BODY,{"disambiguationData":[OSD([sQuery(id+"F0.wireOp",EDGE,"E1")])]}),"instanceName":"1"}),"instanceName":"1"});
            var Q772;
            Q772=makeQuery(id+"F12.opPattern","COPY",BODY,{"derivedFrom":makeQuery(id+"F4.opPattern","COPY",BODY,{"derivedFrom":makeQuery(id+"F2.opPattern","COPY",BODY,{"derivedFrom":makeQuery(id+"F1.opRevolve","SWEPT_BODY",BODY,{"disambiguationData":[OSD([sQuery(id+"F0.wireOp",EDGE,"E1")])]}),"instanceName":"1"}),"instanceName":"1"}),"instanceName":"1"});
            var Q773;
            Q773=makeQuery(id+"F12.opPattern","COPY",BODY,{"derivedFrom":makeQuery(id+"F4.opPattern","COPY",BODY,{"derivedFrom":makeQuery(id+"F3.opPattern","COPY",BODY,{"derivedFrom":makeQuery(id+"F2.opPattern","COPY",BODY,{"derivedFrom":makeQuery(id+"F1.opRevolve","SWEPT_BODY",BODY,{"disambiguationData":[OSD([sQuery(id+"F0.wireOp",EDGE,"E1")])]}),"instanceName":"1"}),"instanceName":"1"}),"instanceName":"1"}),"instanceName":"1"});
            var Q774;
            Q774=makeQuery(id+"F12.opPattern","COPY",BODY,{"derivedFrom":makeQuery(id+"F5.opPattern","COPY",BODY,{"derivedFrom":makeQuery(id+"F1.opRevolve","SWEPT_BODY",BODY,{"disambiguationData":[OSD([sQuery(id+"F0.wireOp",EDGE,"E1")])]}),"instanceName":"1"}),"instanceName":"1"});
            var Q775;
            Q775=makeQuery(id+"F12.opPattern","COPY",BODY,{"derivedFrom":makeQuery(id+"F5.opPattern","COPY",BODY,{"derivedFrom":makeQuery(id+"F2.opPattern","COPY",BODY,{"derivedFrom":makeQuery(id+"F1.opRevolve","SWEPT_BODY",BODY,{"disambiguationData":[OSD([sQuery(id+"F0.wireOp",EDGE,"E1")])]}),"instanceName":"1"}),"instanceName":"1"}),"instanceName":"1"});
            var Q776;
            Q776=makeQuery(id+"F12.opPattern","COPY",BODY,{"derivedFrom":makeQuery(id+"F5.opPattern","COPY",BODY,{"derivedFrom":makeQuery(id+"F3.opPattern","COPY",BODY,{"derivedFrom":makeQuery(id+"F2.opPattern","COPY",BODY,{"derivedFrom":makeQuery(id+"F1.opRevolve","SWEPT_BODY",BODY,{"disambiguationData":[OSD([sQuery(id+"F0.wireOp",EDGE,"E1")])]}),"instanceName":"1"}),"instanceName":"1"}),"instanceName":"1"}),"instanceName":"1"});
            var Q777;
            Q777=makeQuery(id+"F12.opPattern","COPY",BODY,{"derivedFrom":makeQuery(id+"F5.opPattern","COPY",BODY,{"derivedFrom":makeQuery(id+"F4.opPattern","COPY",BODY,{"derivedFrom":makeQuery(id+"F1.opRevolve","SWEPT_BODY",BODY,{"disambiguationData":[OSD([sQuery(id+"F0.wireOp",EDGE,"E1")])]}),"instanceName":"1"}),"instanceName":"1"}),"instanceName":"1"});
            var Q778;
            Q778=makeQuery(id+"F12.opPattern","COPY",BODY,{"derivedFrom":makeQuery(id+"F5.opPattern","COPY",BODY,{"derivedFrom":makeQuery(id+"F4.opPattern","COPY",BODY,{"derivedFrom":makeQuery(id+"F2.opPattern","COPY",BODY,{"derivedFrom":makeQuery(id+"F1.opRevolve","SWEPT_BODY",BODY,{"disambiguationData":[OSD([sQuery(id+"F0.wireOp",EDGE,"E1")])]}),"instanceName":"1"}),"instanceName":"1"}),"instanceName":"1"}),"instanceName":"1"});
            var Q779;
            Q779=makeQuery(id+"F12.opPattern","COPY",BODY,{"derivedFrom":makeQuery(id+"F5.opPattern","COPY",BODY,{"derivedFrom":makeQuery(id+"F4.opPattern","COPY",BODY,{"derivedFrom":makeQuery(id+"F3.opPattern","COPY",BODY,{"derivedFrom":makeQuery(id+"F2.opPattern","COPY",BODY,{"derivedFrom":makeQuery(id+"F1.opRevolve","SWEPT_BODY",BODY,{"disambiguationData":[OSD([sQuery(id+"F0.wireOp",EDGE,"E1")])]}),"instanceName":"1"}),"instanceName":"1"}),"instanceName":"1"}),"instanceName":"1"}),"instanceName":"1"});
            var Q780;
            Q780=makeQuery(id+"F12.opPattern","COPY",BODY,{"derivedFrom":makeQuery(id+"F6.opPattern","COPY",BODY,{"derivedFrom":makeQuery(id+"F1.opRevolve","SWEPT_BODY",BODY,{"disambiguationData":[OSD([sQuery(id+"F0.wireOp",EDGE,"E1")])]}),"instanceName":"1"}),"instanceName":"1"});
            var Q781;
            Q781=makeQuery(id+"F12.opPattern","COPY",BODY,{"derivedFrom":makeQuery(id+"F6.opPattern","COPY",BODY,{"derivedFrom":makeQuery(id+"F2.opPattern","COPY",BODY,{"derivedFrom":makeQuery(id+"F1.opRevolve","SWEPT_BODY",BODY,{"disambiguationData":[OSD([sQuery(id+"F0.wireOp",EDGE,"E1")])]}),"instanceName":"1"}),"instanceName":"1"}),"instanceName":"1"});
            var Q782;
            Q782=makeQuery(id+"F12.opPattern","COPY",BODY,{"derivedFrom":makeQuery(id+"F6.opPattern","COPY",BODY,{"derivedFrom":makeQuery(id+"F3.opPattern","COPY",BODY,{"derivedFrom":makeQuery(id+"F2.opPattern","COPY",BODY,{"derivedFrom":makeQuery(id+"F1.opRevolve","SWEPT_BODY",BODY,{"disambiguationData":[OSD([sQuery(id+"F0.wireOp",EDGE,"E1")])]}),"instanceName":"1"}),"instanceName":"1"}),"instanceName":"1"}),"instanceName":"1"});
            var Q783;
            Q783=makeQuery(id+"F12.opPattern","COPY",BODY,{"derivedFrom":makeQuery(id+"F6.opPattern","COPY",BODY,{"derivedFrom":makeQuery(id+"F4.opPattern","COPY",BODY,{"derivedFrom":makeQuery(id+"F1.opRevolve","SWEPT_BODY",BODY,{"disambiguationData":[OSD([sQuery(id+"F0.wireOp",EDGE,"E1")])]}),"instanceName":"1"}),"instanceName":"1"}),"instanceName":"1"});
            var Q784;
            Q784=makeQuery(id+"F12.opPattern","COPY",BODY,{"derivedFrom":makeQuery(id+"F6.opPattern","COPY",BODY,{"derivedFrom":makeQuery(id+"F4.opPattern","COPY",BODY,{"derivedFrom":makeQuery(id+"F2.opPattern","COPY",BODY,{"derivedFrom":makeQuery(id+"F1.opRevolve","SWEPT_BODY",BODY,{"disambiguationData":[OSD([sQuery(id+"F0.wireOp",EDGE,"E1")])]}),"instanceName":"1"}),"instanceName":"1"}),"instanceName":"1"}),"instanceName":"1"});
            var Q785;
            Q785=makeQuery(id+"F12.opPattern","COPY",BODY,{"derivedFrom":makeQuery(id+"F6.opPattern","COPY",BODY,{"derivedFrom":makeQuery(id+"F4.opPattern","COPY",BODY,{"derivedFrom":makeQuery(id+"F3.opPattern","COPY",BODY,{"derivedFrom":makeQuery(id+"F2.opPattern","COPY",BODY,{"derivedFrom":makeQuery(id+"F1.opRevolve","SWEPT_BODY",BODY,{"disambiguationData":[OSD([sQuery(id+"F0.wireOp",EDGE,"E1")])]}),"instanceName":"1"}),"instanceName":"1"}),"instanceName":"1"}),"instanceName":"1"}),"instanceName":"1"});
            var Q786;
            Q786=makeQuery(id+"F12.opPattern","COPY",BODY,{"derivedFrom":makeQuery(id+"F6.opPattern","COPY",BODY,{"derivedFrom":makeQuery(id+"F5.opPattern","COPY",BODY,{"derivedFrom":makeQuery(id+"F1.opRevolve","SWEPT_BODY",BODY,{"disambiguationData":[OSD([sQuery(id+"F0.wireOp",EDGE,"E1")])]}),"instanceName":"1"}),"instanceName":"1"}),"instanceName":"1"});
            var Q787;
            Q787=makeQuery(id+"F12.opPattern","COPY",BODY,{"derivedFrom":makeQuery(id+"F6.opPattern","COPY",BODY,{"derivedFrom":makeQuery(id+"F5.opPattern","COPY",BODY,{"derivedFrom":makeQuery(id+"F2.opPattern","COPY",BODY,{"derivedFrom":makeQuery(id+"F1.opRevolve","SWEPT_BODY",BODY,{"disambiguationData":[OSD([sQuery(id+"F0.wireOp",EDGE,"E1")])]}),"instanceName":"1"}),"instanceName":"1"}),"instanceName":"1"}),"instanceName":"1"});
            var Q788;
            Q788=makeQuery(id+"F12.opPattern","COPY",BODY,{"derivedFrom":makeQuery(id+"F6.opPattern","COPY",BODY,{"derivedFrom":makeQuery(id+"F5.opPattern","COPY",BODY,{"derivedFrom":makeQuery(id+"F3.opPattern","COPY",BODY,{"derivedFrom":makeQuery(id+"F2.opPattern","COPY",BODY,{"derivedFrom":makeQuery(id+"F1.opRevolve","SWEPT_BODY",BODY,{"disambiguationData":[OSD([sQuery(id+"F0.wireOp",EDGE,"E1")])]}),"instanceName":"1"}),"instanceName":"1"}),"instanceName":"1"}),"instanceName":"1"}),"instanceName":"1"});
            var Q789;
            Q789=makeQuery(id+"F12.opPattern","COPY",BODY,{"derivedFrom":makeQuery(id+"F6.opPattern","COPY",BODY,{"derivedFrom":makeQuery(id+"F5.opPattern","COPY",BODY,{"derivedFrom":makeQuery(id+"F4.opPattern","COPY",BODY,{"derivedFrom":makeQuery(id+"F1.opRevolve","SWEPT_BODY",BODY,{"disambiguationData":[OSD([sQuery(id+"F0.wireOp",EDGE,"E1")])]}),"instanceName":"1"}),"instanceName":"1"}),"instanceName":"1"}),"instanceName":"1"});
            var Q790;
            Q790=makeQuery(id+"F12.opPattern","COPY",BODY,{"derivedFrom":makeQuery(id+"F6.opPattern","COPY",BODY,{"derivedFrom":makeQuery(id+"F5.opPattern","COPY",BODY,{"derivedFrom":makeQuery(id+"F4.opPattern","COPY",BODY,{"derivedFrom":makeQuery(id+"F2.opPattern","COPY",BODY,{"derivedFrom":makeQuery(id+"F1.opRevolve","SWEPT_BODY",BODY,{"disambiguationData":[OSD([sQuery(id+"F0.wireOp",EDGE,"E1")])]}),"instanceName":"1"}),"instanceName":"1"}),"instanceName":"1"}),"instanceName":"1"}),"instanceName":"1"});
            var Q791;
            Q791=makeQuery(id+"F12.opPattern","COPY",BODY,{"derivedFrom":makeQuery(id+"F6.opPattern","COPY",BODY,{"derivedFrom":makeQuery(id+"F5.opPattern","COPY",BODY,{"derivedFrom":makeQuery(id+"F4.opPattern","COPY",BODY,{"derivedFrom":makeQuery(id+"F3.opPattern","COPY",BODY,{"derivedFrom":makeQuery(id+"F2.opPattern","COPY",BODY,{"derivedFrom":makeQuery(id+"F1.opRevolve","SWEPT_BODY",BODY,{"disambiguationData":[OSD([sQuery(id+"F0.wireOp",EDGE,"E1")])]}),"instanceName":"1"}),"instanceName":"1"}),"instanceName":"1"}),"instanceName":"1"}),"instanceName":"1"}),"instanceName":"1"});
            var Q792;
            Q792=makeQuery(id+"F12.opPattern","COPY",BODY,{"derivedFrom":makeQuery(id+"F7.opPattern","COPY",BODY,{"derivedFrom":makeQuery(id+"F1.opRevolve","SWEPT_BODY",BODY,{"disambiguationData":[OSD([sQuery(id+"F0.wireOp",EDGE,"E1")])]}),"instanceName":"1"}),"instanceName":"1"});
            var Q793;
            Q793=makeQuery(id+"F12.opPattern","COPY",BODY,{"derivedFrom":makeQuery(id+"F7.opPattern","COPY",BODY,{"derivedFrom":makeQuery(id+"F2.opPattern","COPY",BODY,{"derivedFrom":makeQuery(id+"F1.opRevolve","SWEPT_BODY",BODY,{"disambiguationData":[OSD([sQuery(id+"F0.wireOp",EDGE,"E1")])]}),"instanceName":"1"}),"instanceName":"1"}),"instanceName":"1"});
            var Q794;
            Q794=makeQuery(id+"F12.opPattern","COPY",BODY,{"derivedFrom":makeQuery(id+"F7.opPattern","COPY",BODY,{"derivedFrom":makeQuery(id+"F3.opPattern","COPY",BODY,{"derivedFrom":makeQuery(id+"F2.opPattern","COPY",BODY,{"derivedFrom":makeQuery(id+"F1.opRevolve","SWEPT_BODY",BODY,{"disambiguationData":[OSD([sQuery(id+"F0.wireOp",EDGE,"E1")])]}),"instanceName":"1"}),"instanceName":"1"}),"instanceName":"1"}),"instanceName":"1"});
            var Q795;
            Q795=makeQuery(id+"F12.opPattern","COPY",BODY,{"derivedFrom":makeQuery(id+"F7.opPattern","COPY",BODY,{"derivedFrom":makeQuery(id+"F4.opPattern","COPY",BODY,{"derivedFrom":makeQuery(id+"F1.opRevolve","SWEPT_BODY",BODY,{"disambiguationData":[OSD([sQuery(id+"F0.wireOp",EDGE,"E1")])]}),"instanceName":"1"}),"instanceName":"1"}),"instanceName":"1"});
            var Q796;
            Q796=makeQuery(id+"F12.opPattern","COPY",BODY,{"derivedFrom":makeQuery(id+"F7.opPattern","COPY",BODY,{"derivedFrom":makeQuery(id+"F4.opPattern","COPY",BODY,{"derivedFrom":makeQuery(id+"F2.opPattern","COPY",BODY,{"derivedFrom":makeQuery(id+"F1.opRevolve","SWEPT_BODY",BODY,{"disambiguationData":[OSD([sQuery(id+"F0.wireOp",EDGE,"E1")])]}),"instanceName":"1"}),"instanceName":"1"}),"instanceName":"1"}),"instanceName":"1"});
            var Q797;
            Q797=makeQuery(id+"F12.opPattern","COPY",BODY,{"derivedFrom":makeQuery(id+"F7.opPattern","COPY",BODY,{"derivedFrom":makeQuery(id+"F4.opPattern","COPY",BODY,{"derivedFrom":makeQuery(id+"F3.opPattern","COPY",BODY,{"derivedFrom":makeQuery(id+"F2.opPattern","COPY",BODY,{"derivedFrom":makeQuery(id+"F1.opRevolve","SWEPT_BODY",BODY,{"disambiguationData":[OSD([sQuery(id+"F0.wireOp",EDGE,"E1")])]}),"instanceName":"1"}),"instanceName":"1"}),"instanceName":"1"}),"instanceName":"1"}),"instanceName":"1"});
            var Q798;
            Q798=makeQuery(id+"F12.opPattern","COPY",BODY,{"derivedFrom":makeQuery(id+"F7.opPattern","COPY",BODY,{"derivedFrom":makeQuery(id+"F5.opPattern","COPY",BODY,{"derivedFrom":makeQuery(id+"F1.opRevolve","SWEPT_BODY",BODY,{"disambiguationData":[OSD([sQuery(id+"F0.wireOp",EDGE,"E1")])]}),"instanceName":"1"}),"instanceName":"1"}),"instanceName":"1"});
            var Q799;
            Q799=makeQuery(id+"F12.opPattern","COPY",BODY,{"derivedFrom":makeQuery(id+"F7.opPattern","COPY",BODY,{"derivedFrom":makeQuery(id+"F5.opPattern","COPY",BODY,{"derivedFrom":makeQuery(id+"F2.opPattern","COPY",BODY,{"derivedFrom":makeQuery(id+"F1.opRevolve","SWEPT_BODY",BODY,{"disambiguationData":[OSD([sQuery(id+"F0.wireOp",EDGE,"E1")])]}),"instanceName":"1"}),"instanceName":"1"}),"instanceName":"1"}),"instanceName":"1"});
            var Q800;
            Q800=makeQuery(id+"F12.opPattern","COPY",BODY,{"derivedFrom":makeQuery(id+"F7.opPattern","COPY",BODY,{"derivedFrom":makeQuery(id+"F5.opPattern","COPY",BODY,{"derivedFrom":makeQuery(id+"F3.opPattern","COPY",BODY,{"derivedFrom":makeQuery(id+"F2.opPattern","COPY",BODY,{"derivedFrom":makeQuery(id+"F1.opRevolve","SWEPT_BODY",BODY,{"disambiguationData":[OSD([sQuery(id+"F0.wireOp",EDGE,"E1")])]}),"instanceName":"1"}),"instanceName":"1"}),"instanceName":"1"}),"instanceName":"1"}),"instanceName":"1"});
            var Q801;
            Q801=makeQuery(id+"F12.opPattern","COPY",BODY,{"derivedFrom":makeQuery(id+"F7.opPattern","COPY",BODY,{"derivedFrom":makeQuery(id+"F5.opPattern","COPY",BODY,{"derivedFrom":makeQuery(id+"F4.opPattern","COPY",BODY,{"derivedFrom":makeQuery(id+"F1.opRevolve","SWEPT_BODY",BODY,{"disambiguationData":[OSD([sQuery(id+"F0.wireOp",EDGE,"E1")])]}),"instanceName":"1"}),"instanceName":"1"}),"instanceName":"1"}),"instanceName":"1"});
            var Q802;
            Q802=makeQuery(id+"F12.opPattern","COPY",BODY,{"derivedFrom":makeQuery(id+"F7.opPattern","COPY",BODY,{"derivedFrom":makeQuery(id+"F5.opPattern","COPY",BODY,{"derivedFrom":makeQuery(id+"F4.opPattern","COPY",BODY,{"derivedFrom":makeQuery(id+"F2.opPattern","COPY",BODY,{"derivedFrom":makeQuery(id+"F1.opRevolve","SWEPT_BODY",BODY,{"disambiguationData":[OSD([sQuery(id+"F0.wireOp",EDGE,"E1")])]}),"instanceName":"1"}),"instanceName":"1"}),"instanceName":"1"}),"instanceName":"1"}),"instanceName":"1"});
            var Q803;
            Q803=makeQuery(id+"F12.opPattern","COPY",BODY,{"derivedFrom":makeQuery(id+"F7.opPattern","COPY",BODY,{"derivedFrom":makeQuery(id+"F5.opPattern","COPY",BODY,{"derivedFrom":makeQuery(id+"F4.opPattern","COPY",BODY,{"derivedFrom":makeQuery(id+"F3.opPattern","COPY",BODY,{"derivedFrom":makeQuery(id+"F2.opPattern","COPY",BODY,{"derivedFrom":makeQuery(id+"F1.opRevolve","SWEPT_BODY",BODY,{"disambiguationData":[OSD([sQuery(id+"F0.wireOp",EDGE,"E1")])]}),"instanceName":"1"}),"instanceName":"1"}),"instanceName":"1"}),"instanceName":"1"}),"instanceName":"1"}),"instanceName":"1"});
            var Q804;
            Q804=makeQuery(id+"F12.opPattern","COPY",BODY,{"derivedFrom":makeQuery(id+"F7.opPattern","COPY",BODY,{"derivedFrom":makeQuery(id+"F6.opPattern","COPY",BODY,{"derivedFrom":makeQuery(id+"F1.opRevolve","SWEPT_BODY",BODY,{"disambiguationData":[OSD([sQuery(id+"F0.wireOp",EDGE,"E1")])]}),"instanceName":"1"}),"instanceName":"1"}),"instanceName":"1"});
            var Q805;
            Q805=makeQuery(id+"F12.opPattern","COPY",BODY,{"derivedFrom":makeQuery(id+"F7.opPattern","COPY",BODY,{"derivedFrom":makeQuery(id+"F6.opPattern","COPY",BODY,{"derivedFrom":makeQuery(id+"F2.opPattern","COPY",BODY,{"derivedFrom":makeQuery(id+"F1.opRevolve","SWEPT_BODY",BODY,{"disambiguationData":[OSD([sQuery(id+"F0.wireOp",EDGE,"E1")])]}),"instanceName":"1"}),"instanceName":"1"}),"instanceName":"1"}),"instanceName":"1"});
            var Q806;
            Q806=makeQuery(id+"F12.opPattern","COPY",BODY,{"derivedFrom":makeQuery(id+"F7.opPattern","COPY",BODY,{"derivedFrom":makeQuery(id+"F6.opPattern","COPY",BODY,{"derivedFrom":makeQuery(id+"F3.opPattern","COPY",BODY,{"derivedFrom":makeQuery(id+"F2.opPattern","COPY",BODY,{"derivedFrom":makeQuery(id+"F1.opRevolve","SWEPT_BODY",BODY,{"disambiguationData":[OSD([sQuery(id+"F0.wireOp",EDGE,"E1")])]}),"instanceName":"1"}),"instanceName":"1"}),"instanceName":"1"}),"instanceName":"1"}),"instanceName":"1"});
            var Q807;
            Q807=makeQuery(id+"F12.opPattern","COPY",BODY,{"derivedFrom":makeQuery(id+"F7.opPattern","COPY",BODY,{"derivedFrom":makeQuery(id+"F6.opPattern","COPY",BODY,{"derivedFrom":makeQuery(id+"F4.opPattern","COPY",BODY,{"derivedFrom":makeQuery(id+"F1.opRevolve","SWEPT_BODY",BODY,{"disambiguationData":[OSD([sQuery(id+"F0.wireOp",EDGE,"E1")])]}),"instanceName":"1"}),"instanceName":"1"}),"instanceName":"1"}),"instanceName":"1"});
            var Q808;
            Q808=makeQuery(id+"F12.opPattern","COPY",BODY,{"derivedFrom":makeQuery(id+"F7.opPattern","COPY",BODY,{"derivedFrom":makeQuery(id+"F6.opPattern","COPY",BODY,{"derivedFrom":makeQuery(id+"F4.opPattern","COPY",BODY,{"derivedFrom":makeQuery(id+"F2.opPattern","COPY",BODY,{"derivedFrom":makeQuery(id+"F1.opRevolve","SWEPT_BODY",BODY,{"disambiguationData":[OSD([sQuery(id+"F0.wireOp",EDGE,"E1")])]}),"instanceName":"1"}),"instanceName":"1"}),"instanceName":"1"}),"instanceName":"1"}),"instanceName":"1"});
            var Q809;
            Q809=makeQuery(id+"F12.opPattern","COPY",BODY,{"derivedFrom":makeQuery(id+"F7.opPattern","COPY",BODY,{"derivedFrom":makeQuery(id+"F6.opPattern","COPY",BODY,{"derivedFrom":makeQuery(id+"F4.opPattern","COPY",BODY,{"derivedFrom":makeQuery(id+"F3.opPattern","COPY",BODY,{"derivedFrom":makeQuery(id+"F2.opPattern","COPY",BODY,{"derivedFrom":makeQuery(id+"F1.opRevolve","SWEPT_BODY",BODY,{"disambiguationData":[OSD([sQuery(id+"F0.wireOp",EDGE,"E1")])]}),"instanceName":"1"}),"instanceName":"1"}),"instanceName":"1"}),"instanceName":"1"}),"instanceName":"1"}),"instanceName":"1"});
            var Q810;
            Q810=makeQuery(id+"F12.opPattern","COPY",BODY,{"derivedFrom":makeQuery(id+"F7.opPattern","COPY",BODY,{"derivedFrom":makeQuery(id+"F6.opPattern","COPY",BODY,{"derivedFrom":makeQuery(id+"F5.opPattern","COPY",BODY,{"derivedFrom":makeQuery(id+"F1.opRevolve","SWEPT_BODY",BODY,{"disambiguationData":[OSD([sQuery(id+"F0.wireOp",EDGE,"E1")])]}),"instanceName":"1"}),"instanceName":"1"}),"instanceName":"1"}),"instanceName":"1"});
            var Q811;
            Q811=makeQuery(id+"F12.opPattern","COPY",BODY,{"derivedFrom":makeQuery(id+"F7.opPattern","COPY",BODY,{"derivedFrom":makeQuery(id+"F6.opPattern","COPY",BODY,{"derivedFrom":makeQuery(id+"F5.opPattern","COPY",BODY,{"derivedFrom":makeQuery(id+"F2.opPattern","COPY",BODY,{"derivedFrom":makeQuery(id+"F1.opRevolve","SWEPT_BODY",BODY,{"disambiguationData":[OSD([sQuery(id+"F0.wireOp",EDGE,"E1")])]}),"instanceName":"1"}),"instanceName":"1"}),"instanceName":"1"}),"instanceName":"1"}),"instanceName":"1"});
            var Q812;
            Q812=makeQuery(id+"F12.opPattern","COPY",BODY,{"derivedFrom":makeQuery(id+"F7.opPattern","COPY",BODY,{"derivedFrom":makeQuery(id+"F6.opPattern","COPY",BODY,{"derivedFrom":makeQuery(id+"F5.opPattern","COPY",BODY,{"derivedFrom":makeQuery(id+"F3.opPattern","COPY",BODY,{"derivedFrom":makeQuery(id+"F2.opPattern","COPY",BODY,{"derivedFrom":makeQuery(id+"F1.opRevolve","SWEPT_BODY",BODY,{"disambiguationData":[OSD([sQuery(id+"F0.wireOp",EDGE,"E1")])]}),"instanceName":"1"}),"instanceName":"1"}),"instanceName":"1"}),"instanceName":"1"}),"instanceName":"1"}),"instanceName":"1"});
            var Q813;
            Q813=makeQuery(id+"F12.opPattern","COPY",BODY,{"derivedFrom":makeQuery(id+"F7.opPattern","COPY",BODY,{"derivedFrom":makeQuery(id+"F6.opPattern","COPY",BODY,{"derivedFrom":makeQuery(id+"F5.opPattern","COPY",BODY,{"derivedFrom":makeQuery(id+"F4.opPattern","COPY",BODY,{"derivedFrom":makeQuery(id+"F1.opRevolve","SWEPT_BODY",BODY,{"disambiguationData":[OSD([sQuery(id+"F0.wireOp",EDGE,"E1")])]}),"instanceName":"1"}),"instanceName":"1"}),"instanceName":"1"}),"instanceName":"1"}),"instanceName":"1"});
            var Q814;
            Q814=makeQuery(id+"F12.opPattern","COPY",BODY,{"derivedFrom":makeQuery(id+"F7.opPattern","COPY",BODY,{"derivedFrom":makeQuery(id+"F6.opPattern","COPY",BODY,{"derivedFrom":makeQuery(id+"F5.opPattern","COPY",BODY,{"derivedFrom":makeQuery(id+"F4.opPattern","COPY",BODY,{"derivedFrom":makeQuery(id+"F2.opPattern","COPY",BODY,{"derivedFrom":makeQuery(id+"F1.opRevolve","SWEPT_BODY",BODY,{"disambiguationData":[OSD([sQuery(id+"F0.wireOp",EDGE,"E1")])]}),"instanceName":"1"}),"instanceName":"1"}),"instanceName":"1"}),"instanceName":"1"}),"instanceName":"1"}),"instanceName":"1"});
            var Q815;
            Q815=makeQuery(id+"F12.opPattern","COPY",BODY,{"derivedFrom":makeQuery(id+"F7.opPattern","COPY",BODY,{"derivedFrom":makeQuery(id+"F6.opPattern","COPY",BODY,{"derivedFrom":makeQuery(id+"F5.opPattern","COPY",BODY,{"derivedFrom":makeQuery(id+"F4.opPattern","COPY",BODY,{"derivedFrom":makeQuery(id+"F3.opPattern","COPY",BODY,{"derivedFrom":makeQuery(id+"F2.opPattern","COPY",BODY,{"derivedFrom":makeQuery(id+"F1.opRevolve","SWEPT_BODY",BODY,{"disambiguationData":[OSD([sQuery(id+"F0.wireOp",EDGE,"E1")])]}),"instanceName":"1"}),"instanceName":"1"}),"instanceName":"1"}),"instanceName":"1"}),"instanceName":"1"}),"instanceName":"1"}),"instanceName":"1"});
            var Q816;
            Q816=makeQuery(id+"F12.opPattern","COPY",BODY,{"derivedFrom":makeQuery(id+"F8.opPattern","COPY",BODY,{"derivedFrom":makeQuery(id+"F1.opRevolve","SWEPT_BODY",BODY,{"disambiguationData":[OSD([sQuery(id+"F0.wireOp",EDGE,"E1")])]}),"instanceName":"1"}),"instanceName":"1"});
            var Q817;
            Q817=makeQuery(id+"F12.opPattern","COPY",BODY,{"derivedFrom":makeQuery(id+"F8.opPattern","COPY",BODY,{"derivedFrom":makeQuery(id+"F2.opPattern","COPY",BODY,{"derivedFrom":makeQuery(id+"F1.opRevolve","SWEPT_BODY",BODY,{"disambiguationData":[OSD([sQuery(id+"F0.wireOp",EDGE,"E1")])]}),"instanceName":"1"}),"instanceName":"1"}),"instanceName":"1"});
            var Q818;
            Q818=makeQuery(id+"F12.opPattern","COPY",BODY,{"derivedFrom":makeQuery(id+"F8.opPattern","COPY",BODY,{"derivedFrom":makeQuery(id+"F3.opPattern","COPY",BODY,{"derivedFrom":makeQuery(id+"F2.opPattern","COPY",BODY,{"derivedFrom":makeQuery(id+"F1.opRevolve","SWEPT_BODY",BODY,{"disambiguationData":[OSD([sQuery(id+"F0.wireOp",EDGE,"E1")])]}),"instanceName":"1"}),"instanceName":"1"}),"instanceName":"1"}),"instanceName":"1"});
            var Q819;
            Q819=makeQuery(id+"F12.opPattern","COPY",BODY,{"derivedFrom":makeQuery(id+"F8.opPattern","COPY",BODY,{"derivedFrom":makeQuery(id+"F4.opPattern","COPY",BODY,{"derivedFrom":makeQuery(id+"F1.opRevolve","SWEPT_BODY",BODY,{"disambiguationData":[OSD([sQuery(id+"F0.wireOp",EDGE,"E1")])]}),"instanceName":"1"}),"instanceName":"1"}),"instanceName":"1"});
            var Q820;
            Q820=makeQuery(id+"F12.opPattern","COPY",BODY,{"derivedFrom":makeQuery(id+"F8.opPattern","COPY",BODY,{"derivedFrom":makeQuery(id+"F4.opPattern","COPY",BODY,{"derivedFrom":makeQuery(id+"F2.opPattern","COPY",BODY,{"derivedFrom":makeQuery(id+"F1.opRevolve","SWEPT_BODY",BODY,{"disambiguationData":[OSD([sQuery(id+"F0.wireOp",EDGE,"E1")])]}),"instanceName":"1"}),"instanceName":"1"}),"instanceName":"1"}),"instanceName":"1"});
            var Q821;
            Q821=makeQuery(id+"F12.opPattern","COPY",BODY,{"derivedFrom":makeQuery(id+"F8.opPattern","COPY",BODY,{"derivedFrom":makeQuery(id+"F4.opPattern","COPY",BODY,{"derivedFrom":makeQuery(id+"F3.opPattern","COPY",BODY,{"derivedFrom":makeQuery(id+"F2.opPattern","COPY",BODY,{"derivedFrom":makeQuery(id+"F1.opRevolve","SWEPT_BODY",BODY,{"disambiguationData":[OSD([sQuery(id+"F0.wireOp",EDGE,"E1")])]}),"instanceName":"1"}),"instanceName":"1"}),"instanceName":"1"}),"instanceName":"1"}),"instanceName":"1"});
            var Q822;
            Q822=makeQuery(id+"F12.opPattern","COPY",BODY,{"derivedFrom":makeQuery(id+"F8.opPattern","COPY",BODY,{"derivedFrom":makeQuery(id+"F5.opPattern","COPY",BODY,{"derivedFrom":makeQuery(id+"F1.opRevolve","SWEPT_BODY",BODY,{"disambiguationData":[OSD([sQuery(id+"F0.wireOp",EDGE,"E1")])]}),"instanceName":"1"}),"instanceName":"1"}),"instanceName":"1"});
            var Q823;
            Q823=makeQuery(id+"F12.opPattern","COPY",BODY,{"derivedFrom":makeQuery(id+"F8.opPattern","COPY",BODY,{"derivedFrom":makeQuery(id+"F5.opPattern","COPY",BODY,{"derivedFrom":makeQuery(id+"F2.opPattern","COPY",BODY,{"derivedFrom":makeQuery(id+"F1.opRevolve","SWEPT_BODY",BODY,{"disambiguationData":[OSD([sQuery(id+"F0.wireOp",EDGE,"E1")])]}),"instanceName":"1"}),"instanceName":"1"}),"instanceName":"1"}),"instanceName":"1"});
            var Q824;
            Q824=makeQuery(id+"F12.opPattern","COPY",BODY,{"derivedFrom":makeQuery(id+"F8.opPattern","COPY",BODY,{"derivedFrom":makeQuery(id+"F5.opPattern","COPY",BODY,{"derivedFrom":makeQuery(id+"F3.opPattern","COPY",BODY,{"derivedFrom":makeQuery(id+"F2.opPattern","COPY",BODY,{"derivedFrom":makeQuery(id+"F1.opRevolve","SWEPT_BODY",BODY,{"disambiguationData":[OSD([sQuery(id+"F0.wireOp",EDGE,"E1")])]}),"instanceName":"1"}),"instanceName":"1"}),"instanceName":"1"}),"instanceName":"1"}),"instanceName":"1"});
            var Q825;
            Q825=makeQuery(id+"F12.opPattern","COPY",BODY,{"derivedFrom":makeQuery(id+"F8.opPattern","COPY",BODY,{"derivedFrom":makeQuery(id+"F5.opPattern","COPY",BODY,{"derivedFrom":makeQuery(id+"F4.opPattern","COPY",BODY,{"derivedFrom":makeQuery(id+"F1.opRevolve","SWEPT_BODY",BODY,{"disambiguationData":[OSD([sQuery(id+"F0.wireOp",EDGE,"E1")])]}),"instanceName":"1"}),"instanceName":"1"}),"instanceName":"1"}),"instanceName":"1"});
            var Q826;
            Q826=makeQuery(id+"F12.opPattern","COPY",BODY,{"derivedFrom":makeQuery(id+"F8.opPattern","COPY",BODY,{"derivedFrom":makeQuery(id+"F5.opPattern","COPY",BODY,{"derivedFrom":makeQuery(id+"F4.opPattern","COPY",BODY,{"derivedFrom":makeQuery(id+"F2.opPattern","COPY",BODY,{"derivedFrom":makeQuery(id+"F1.opRevolve","SWEPT_BODY",BODY,{"disambiguationData":[OSD([sQuery(id+"F0.wireOp",EDGE,"E1")])]}),"instanceName":"1"}),"instanceName":"1"}),"instanceName":"1"}),"instanceName":"1"}),"instanceName":"1"});
            var Q827;
            Q827=makeQuery(id+"F12.opPattern","COPY",BODY,{"derivedFrom":makeQuery(id+"F8.opPattern","COPY",BODY,{"derivedFrom":makeQuery(id+"F5.opPattern","COPY",BODY,{"derivedFrom":makeQuery(id+"F4.opPattern","COPY",BODY,{"derivedFrom":makeQuery(id+"F3.opPattern","COPY",BODY,{"derivedFrom":makeQuery(id+"F2.opPattern","COPY",BODY,{"derivedFrom":makeQuery(id+"F1.opRevolve","SWEPT_BODY",BODY,{"disambiguationData":[OSD([sQuery(id+"F0.wireOp",EDGE,"E1")])]}),"instanceName":"1"}),"instanceName":"1"}),"instanceName":"1"}),"instanceName":"1"}),"instanceName":"1"}),"instanceName":"1"});
            var Q828;
            Q828=makeQuery(id+"F12.opPattern","COPY",BODY,{"derivedFrom":makeQuery(id+"F8.opPattern","COPY",BODY,{"derivedFrom":makeQuery(id+"F6.opPattern","COPY",BODY,{"derivedFrom":makeQuery(id+"F1.opRevolve","SWEPT_BODY",BODY,{"disambiguationData":[OSD([sQuery(id+"F0.wireOp",EDGE,"E1")])]}),"instanceName":"1"}),"instanceName":"1"}),"instanceName":"1"});
            var Q829;
            Q829=makeQuery(id+"F12.opPattern","COPY",BODY,{"derivedFrom":makeQuery(id+"F8.opPattern","COPY",BODY,{"derivedFrom":makeQuery(id+"F6.opPattern","COPY",BODY,{"derivedFrom":makeQuery(id+"F2.opPattern","COPY",BODY,{"derivedFrom":makeQuery(id+"F1.opRevolve","SWEPT_BODY",BODY,{"disambiguationData":[OSD([sQuery(id+"F0.wireOp",EDGE,"E1")])]}),"instanceName":"1"}),"instanceName":"1"}),"instanceName":"1"}),"instanceName":"1"});
            var Q830;
            Q830=makeQuery(id+"F12.opPattern","COPY",BODY,{"derivedFrom":makeQuery(id+"F8.opPattern","COPY",BODY,{"derivedFrom":makeQuery(id+"F6.opPattern","COPY",BODY,{"derivedFrom":makeQuery(id+"F3.opPattern","COPY",BODY,{"derivedFrom":makeQuery(id+"F2.opPattern","COPY",BODY,{"derivedFrom":makeQuery(id+"F1.opRevolve","SWEPT_BODY",BODY,{"disambiguationData":[OSD([sQuery(id+"F0.wireOp",EDGE,"E1")])]}),"instanceName":"1"}),"instanceName":"1"}),"instanceName":"1"}),"instanceName":"1"}),"instanceName":"1"});
            var Q831;
            Q831=makeQuery(id+"F12.opPattern","COPY",BODY,{"derivedFrom":makeQuery(id+"F8.opPattern","COPY",BODY,{"derivedFrom":makeQuery(id+"F6.opPattern","COPY",BODY,{"derivedFrom":makeQuery(id+"F4.opPattern","COPY",BODY,{"derivedFrom":makeQuery(id+"F1.opRevolve","SWEPT_BODY",BODY,{"disambiguationData":[OSD([sQuery(id+"F0.wireOp",EDGE,"E1")])]}),"instanceName":"1"}),"instanceName":"1"}),"instanceName":"1"}),"instanceName":"1"});
            var Q832;
            Q832=makeQuery(id+"F12.opPattern","COPY",BODY,{"derivedFrom":makeQuery(id+"F8.opPattern","COPY",BODY,{"derivedFrom":makeQuery(id+"F6.opPattern","COPY",BODY,{"derivedFrom":makeQuery(id+"F4.opPattern","COPY",BODY,{"derivedFrom":makeQuery(id+"F2.opPattern","COPY",BODY,{"derivedFrom":makeQuery(id+"F1.opRevolve","SWEPT_BODY",BODY,{"disambiguationData":[OSD([sQuery(id+"F0.wireOp",EDGE,"E1")])]}),"instanceName":"1"}),"instanceName":"1"}),"instanceName":"1"}),"instanceName":"1"}),"instanceName":"1"});
            var Q833;
            Q833=makeQuery(id+"F12.opPattern","COPY",BODY,{"derivedFrom":makeQuery(id+"F8.opPattern","COPY",BODY,{"derivedFrom":makeQuery(id+"F6.opPattern","COPY",BODY,{"derivedFrom":makeQuery(id+"F4.opPattern","COPY",BODY,{"derivedFrom":makeQuery(id+"F3.opPattern","COPY",BODY,{"derivedFrom":makeQuery(id+"F2.opPattern","COPY",BODY,{"derivedFrom":makeQuery(id+"F1.opRevolve","SWEPT_BODY",BODY,{"disambiguationData":[OSD([sQuery(id+"F0.wireOp",EDGE,"E1")])]}),"instanceName":"1"}),"instanceName":"1"}),"instanceName":"1"}),"instanceName":"1"}),"instanceName":"1"}),"instanceName":"1"});
            var Q834;
            Q834=makeQuery(id+"F12.opPattern","COPY",BODY,{"derivedFrom":makeQuery(id+"F8.opPattern","COPY",BODY,{"derivedFrom":makeQuery(id+"F6.opPattern","COPY",BODY,{"derivedFrom":makeQuery(id+"F5.opPattern","COPY",BODY,{"derivedFrom":makeQuery(id+"F1.opRevolve","SWEPT_BODY",BODY,{"disambiguationData":[OSD([sQuery(id+"F0.wireOp",EDGE,"E1")])]}),"instanceName":"1"}),"instanceName":"1"}),"instanceName":"1"}),"instanceName":"1"});
            var Q835;
            Q835=makeQuery(id+"F12.opPattern","COPY",BODY,{"derivedFrom":makeQuery(id+"F8.opPattern","COPY",BODY,{"derivedFrom":makeQuery(id+"F6.opPattern","COPY",BODY,{"derivedFrom":makeQuery(id+"F5.opPattern","COPY",BODY,{"derivedFrom":makeQuery(id+"F2.opPattern","COPY",BODY,{"derivedFrom":makeQuery(id+"F1.opRevolve","SWEPT_BODY",BODY,{"disambiguationData":[OSD([sQuery(id+"F0.wireOp",EDGE,"E1")])]}),"instanceName":"1"}),"instanceName":"1"}),"instanceName":"1"}),"instanceName":"1"}),"instanceName":"1"});
            var Q836;
            Q836=makeQuery(id+"F12.opPattern","COPY",BODY,{"derivedFrom":makeQuery(id+"F8.opPattern","COPY",BODY,{"derivedFrom":makeQuery(id+"F6.opPattern","COPY",BODY,{"derivedFrom":makeQuery(id+"F5.opPattern","COPY",BODY,{"derivedFrom":makeQuery(id+"F3.opPattern","COPY",BODY,{"derivedFrom":makeQuery(id+"F2.opPattern","COPY",BODY,{"derivedFrom":makeQuery(id+"F1.opRevolve","SWEPT_BODY",BODY,{"disambiguationData":[OSD([sQuery(id+"F0.wireOp",EDGE,"E1")])]}),"instanceName":"1"}),"instanceName":"1"}),"instanceName":"1"}),"instanceName":"1"}),"instanceName":"1"}),"instanceName":"1"});
            var Q837;
            Q837=makeQuery(id+"F12.opPattern","COPY",BODY,{"derivedFrom":makeQuery(id+"F8.opPattern","COPY",BODY,{"derivedFrom":makeQuery(id+"F6.opPattern","COPY",BODY,{"derivedFrom":makeQuery(id+"F5.opPattern","COPY",BODY,{"derivedFrom":makeQuery(id+"F4.opPattern","COPY",BODY,{"derivedFrom":makeQuery(id+"F1.opRevolve","SWEPT_BODY",BODY,{"disambiguationData":[OSD([sQuery(id+"F0.wireOp",EDGE,"E1")])]}),"instanceName":"1"}),"instanceName":"1"}),"instanceName":"1"}),"instanceName":"1"}),"instanceName":"1"});
            var Q838;
            Q838=makeQuery(id+"F12.opPattern","COPY",BODY,{"derivedFrom":makeQuery(id+"F8.opPattern","COPY",BODY,{"derivedFrom":makeQuery(id+"F6.opPattern","COPY",BODY,{"derivedFrom":makeQuery(id+"F5.opPattern","COPY",BODY,{"derivedFrom":makeQuery(id+"F4.opPattern","COPY",BODY,{"derivedFrom":makeQuery(id+"F2.opPattern","COPY",BODY,{"derivedFrom":makeQuery(id+"F1.opRevolve","SWEPT_BODY",BODY,{"disambiguationData":[OSD([sQuery(id+"F0.wireOp",EDGE,"E1")])]}),"instanceName":"1"}),"instanceName":"1"}),"instanceName":"1"}),"instanceName":"1"}),"instanceName":"1"}),"instanceName":"1"});
            var Q839;
            Q839=makeQuery(id+"F12.opPattern","COPY",BODY,{"derivedFrom":makeQuery(id+"F8.opPattern","COPY",BODY,{"derivedFrom":makeQuery(id+"F6.opPattern","COPY",BODY,{"derivedFrom":makeQuery(id+"F5.opPattern","COPY",BODY,{"derivedFrom":makeQuery(id+"F4.opPattern","COPY",BODY,{"derivedFrom":makeQuery(id+"F3.opPattern","COPY",BODY,{"derivedFrom":makeQuery(id+"F2.opPattern","COPY",BODY,{"derivedFrom":makeQuery(id+"F1.opRevolve","SWEPT_BODY",BODY,{"disambiguationData":[OSD([sQuery(id+"F0.wireOp",EDGE,"E1")])]}),"instanceName":"1"}),"instanceName":"1"}),"instanceName":"1"}),"instanceName":"1"}),"instanceName":"1"}),"instanceName":"1"}),"instanceName":"1"});
            var Q840;
            Q840=makeQuery(id+"F12.opPattern","COPY",BODY,{"derivedFrom":makeQuery(id+"F8.opPattern","COPY",BODY,{"derivedFrom":makeQuery(id+"F7.opPattern","COPY",BODY,{"derivedFrom":makeQuery(id+"F1.opRevolve","SWEPT_BODY",BODY,{"disambiguationData":[OSD([sQuery(id+"F0.wireOp",EDGE,"E1")])]}),"instanceName":"1"}),"instanceName":"1"}),"instanceName":"1"});
            var Q841;
            Q841=makeQuery(id+"F12.opPattern","COPY",BODY,{"derivedFrom":makeQuery(id+"F8.opPattern","COPY",BODY,{"derivedFrom":makeQuery(id+"F7.opPattern","COPY",BODY,{"derivedFrom":makeQuery(id+"F2.opPattern","COPY",BODY,{"derivedFrom":makeQuery(id+"F1.opRevolve","SWEPT_BODY",BODY,{"disambiguationData":[OSD([sQuery(id+"F0.wireOp",EDGE,"E1")])]}),"instanceName":"1"}),"instanceName":"1"}),"instanceName":"1"}),"instanceName":"1"});
            var Q842;
            Q842=makeQuery(id+"F12.opPattern","COPY",BODY,{"derivedFrom":makeQuery(id+"F8.opPattern","COPY",BODY,{"derivedFrom":makeQuery(id+"F7.opPattern","COPY",BODY,{"derivedFrom":makeQuery(id+"F3.opPattern","COPY",BODY,{"derivedFrom":makeQuery(id+"F2.opPattern","COPY",BODY,{"derivedFrom":makeQuery(id+"F1.opRevolve","SWEPT_BODY",BODY,{"disambiguationData":[OSD([sQuery(id+"F0.wireOp",EDGE,"E1")])]}),"instanceName":"1"}),"instanceName":"1"}),"instanceName":"1"}),"instanceName":"1"}),"instanceName":"1"});
            var Q843;
            Q843=makeQuery(id+"F12.opPattern","COPY",BODY,{"derivedFrom":makeQuery(id+"F8.opPattern","COPY",BODY,{"derivedFrom":makeQuery(id+"F7.opPattern","COPY",BODY,{"derivedFrom":makeQuery(id+"F4.opPattern","COPY",BODY,{"derivedFrom":makeQuery(id+"F1.opRevolve","SWEPT_BODY",BODY,{"disambiguationData":[OSD([sQuery(id+"F0.wireOp",EDGE,"E1")])]}),"instanceName":"1"}),"instanceName":"1"}),"instanceName":"1"}),"instanceName":"1"});
            var Q844;
            Q844=makeQuery(id+"F12.opPattern","COPY",BODY,{"derivedFrom":makeQuery(id+"F8.opPattern","COPY",BODY,{"derivedFrom":makeQuery(id+"F7.opPattern","COPY",BODY,{"derivedFrom":makeQuery(id+"F4.opPattern","COPY",BODY,{"derivedFrom":makeQuery(id+"F2.opPattern","COPY",BODY,{"derivedFrom":makeQuery(id+"F1.opRevolve","SWEPT_BODY",BODY,{"disambiguationData":[OSD([sQuery(id+"F0.wireOp",EDGE,"E1")])]}),"instanceName":"1"}),"instanceName":"1"}),"instanceName":"1"}),"instanceName":"1"}),"instanceName":"1"});
            var Q845;
            Q845=makeQuery(id+"F12.opPattern","COPY",BODY,{"derivedFrom":makeQuery(id+"F8.opPattern","COPY",BODY,{"derivedFrom":makeQuery(id+"F7.opPattern","COPY",BODY,{"derivedFrom":makeQuery(id+"F4.opPattern","COPY",BODY,{"derivedFrom":makeQuery(id+"F3.opPattern","COPY",BODY,{"derivedFrom":makeQuery(id+"F2.opPattern","COPY",BODY,{"derivedFrom":makeQuery(id+"F1.opRevolve","SWEPT_BODY",BODY,{"disambiguationData":[OSD([sQuery(id+"F0.wireOp",EDGE,"E1")])]}),"instanceName":"1"}),"instanceName":"1"}),"instanceName":"1"}),"instanceName":"1"}),"instanceName":"1"}),"instanceName":"1"});
            var Q846;
            Q846=makeQuery(id+"F12.opPattern","COPY",BODY,{"derivedFrom":makeQuery(id+"F8.opPattern","COPY",BODY,{"derivedFrom":makeQuery(id+"F7.opPattern","COPY",BODY,{"derivedFrom":makeQuery(id+"F5.opPattern","COPY",BODY,{"derivedFrom":makeQuery(id+"F1.opRevolve","SWEPT_BODY",BODY,{"disambiguationData":[OSD([sQuery(id+"F0.wireOp",EDGE,"E1")])]}),"instanceName":"1"}),"instanceName":"1"}),"instanceName":"1"}),"instanceName":"1"});
            var Q847;
            Q847=makeQuery(id+"F12.opPattern","COPY",BODY,{"derivedFrom":makeQuery(id+"F8.opPattern","COPY",BODY,{"derivedFrom":makeQuery(id+"F7.opPattern","COPY",BODY,{"derivedFrom":makeQuery(id+"F5.opPattern","COPY",BODY,{"derivedFrom":makeQuery(id+"F2.opPattern","COPY",BODY,{"derivedFrom":makeQuery(id+"F1.opRevolve","SWEPT_BODY",BODY,{"disambiguationData":[OSD([sQuery(id+"F0.wireOp",EDGE,"E1")])]}),"instanceName":"1"}),"instanceName":"1"}),"instanceName":"1"}),"instanceName":"1"}),"instanceName":"1"});
            var Q848;
            Q848=makeQuery(id+"F12.opPattern","COPY",BODY,{"derivedFrom":makeQuery(id+"F8.opPattern","COPY",BODY,{"derivedFrom":makeQuery(id+"F7.opPattern","COPY",BODY,{"derivedFrom":makeQuery(id+"F5.opPattern","COPY",BODY,{"derivedFrom":makeQuery(id+"F3.opPattern","COPY",BODY,{"derivedFrom":makeQuery(id+"F2.opPattern","COPY",BODY,{"derivedFrom":makeQuery(id+"F1.opRevolve","SWEPT_BODY",BODY,{"disambiguationData":[OSD([sQuery(id+"F0.wireOp",EDGE,"E1")])]}),"instanceName":"1"}),"instanceName":"1"}),"instanceName":"1"}),"instanceName":"1"}),"instanceName":"1"}),"instanceName":"1"});
            var Q849;
            Q849=makeQuery(id+"F12.opPattern","COPY",BODY,{"derivedFrom":makeQuery(id+"F8.opPattern","COPY",BODY,{"derivedFrom":makeQuery(id+"F7.opPattern","COPY",BODY,{"derivedFrom":makeQuery(id+"F5.opPattern","COPY",BODY,{"derivedFrom":makeQuery(id+"F4.opPattern","COPY",BODY,{"derivedFrom":makeQuery(id+"F1.opRevolve","SWEPT_BODY",BODY,{"disambiguationData":[OSD([sQuery(id+"F0.wireOp",EDGE,"E1")])]}),"instanceName":"1"}),"instanceName":"1"}),"instanceName":"1"}),"instanceName":"1"}),"instanceName":"1"});
            var Q850;
            Q850=makeQuery(id+"F12.opPattern","COPY",BODY,{"derivedFrom":makeQuery(id+"F8.opPattern","COPY",BODY,{"derivedFrom":makeQuery(id+"F7.opPattern","COPY",BODY,{"derivedFrom":makeQuery(id+"F5.opPattern","COPY",BODY,{"derivedFrom":makeQuery(id+"F4.opPattern","COPY",BODY,{"derivedFrom":makeQuery(id+"F2.opPattern","COPY",BODY,{"derivedFrom":makeQuery(id+"F1.opRevolve","SWEPT_BODY",BODY,{"disambiguationData":[OSD([sQuery(id+"F0.wireOp",EDGE,"E1")])]}),"instanceName":"1"}),"instanceName":"1"}),"instanceName":"1"}),"instanceName":"1"}),"instanceName":"1"}),"instanceName":"1"});
            var Q851;
            Q851=makeQuery(id+"F12.opPattern","COPY",BODY,{"derivedFrom":makeQuery(id+"F8.opPattern","COPY",BODY,{"derivedFrom":makeQuery(id+"F7.opPattern","COPY",BODY,{"derivedFrom":makeQuery(id+"F5.opPattern","COPY",BODY,{"derivedFrom":makeQuery(id+"F4.opPattern","COPY",BODY,{"derivedFrom":makeQuery(id+"F3.opPattern","COPY",BODY,{"derivedFrom":makeQuery(id+"F2.opPattern","COPY",BODY,{"derivedFrom":makeQuery(id+"F1.opRevolve","SWEPT_BODY",BODY,{"disambiguationData":[OSD([sQuery(id+"F0.wireOp",EDGE,"E1")])]}),"instanceName":"1"}),"instanceName":"1"}),"instanceName":"1"}),"instanceName":"1"}),"instanceName":"1"}),"instanceName":"1"}),"instanceName":"1"});
            var Q852;
            Q852=makeQuery(id+"F12.opPattern","COPY",BODY,{"derivedFrom":makeQuery(id+"F8.opPattern","COPY",BODY,{"derivedFrom":makeQuery(id+"F7.opPattern","COPY",BODY,{"derivedFrom":makeQuery(id+"F6.opPattern","COPY",BODY,{"derivedFrom":makeQuery(id+"F1.opRevolve","SWEPT_BODY",BODY,{"disambiguationData":[OSD([sQuery(id+"F0.wireOp",EDGE,"E1")])]}),"instanceName":"1"}),"instanceName":"1"}),"instanceName":"1"}),"instanceName":"1"});
            var Q853;
            Q853=makeQuery(id+"F12.opPattern","COPY",BODY,{"derivedFrom":makeQuery(id+"F8.opPattern","COPY",BODY,{"derivedFrom":makeQuery(id+"F7.opPattern","COPY",BODY,{"derivedFrom":makeQuery(id+"F6.opPattern","COPY",BODY,{"derivedFrom":makeQuery(id+"F2.opPattern","COPY",BODY,{"derivedFrom":makeQuery(id+"F1.opRevolve","SWEPT_BODY",BODY,{"disambiguationData":[OSD([sQuery(id+"F0.wireOp",EDGE,"E1")])]}),"instanceName":"1"}),"instanceName":"1"}),"instanceName":"1"}),"instanceName":"1"}),"instanceName":"1"});
            var Q854;
            Q854=makeQuery(id+"F12.opPattern","COPY",BODY,{"derivedFrom":makeQuery(id+"F8.opPattern","COPY",BODY,{"derivedFrom":makeQuery(id+"F7.opPattern","COPY",BODY,{"derivedFrom":makeQuery(id+"F6.opPattern","COPY",BODY,{"derivedFrom":makeQuery(id+"F3.opPattern","COPY",BODY,{"derivedFrom":makeQuery(id+"F2.opPattern","COPY",BODY,{"derivedFrom":makeQuery(id+"F1.opRevolve","SWEPT_BODY",BODY,{"disambiguationData":[OSD([sQuery(id+"F0.wireOp",EDGE,"E1")])]}),"instanceName":"1"}),"instanceName":"1"}),"instanceName":"1"}),"instanceName":"1"}),"instanceName":"1"}),"instanceName":"1"});
            var Q855;
            Q855=makeQuery(id+"F12.opPattern","COPY",BODY,{"derivedFrom":makeQuery(id+"F8.opPattern","COPY",BODY,{"derivedFrom":makeQuery(id+"F7.opPattern","COPY",BODY,{"derivedFrom":makeQuery(id+"F6.opPattern","COPY",BODY,{"derivedFrom":makeQuery(id+"F4.opPattern","COPY",BODY,{"derivedFrom":makeQuery(id+"F1.opRevolve","SWEPT_BODY",BODY,{"disambiguationData":[OSD([sQuery(id+"F0.wireOp",EDGE,"E1")])]}),"instanceName":"1"}),"instanceName":"1"}),"instanceName":"1"}),"instanceName":"1"}),"instanceName":"1"});
            var Q856;
            Q856=makeQuery(id+"F12.opPattern","COPY",BODY,{"derivedFrom":makeQuery(id+"F8.opPattern","COPY",BODY,{"derivedFrom":makeQuery(id+"F7.opPattern","COPY",BODY,{"derivedFrom":makeQuery(id+"F6.opPattern","COPY",BODY,{"derivedFrom":makeQuery(id+"F4.opPattern","COPY",BODY,{"derivedFrom":makeQuery(id+"F2.opPattern","COPY",BODY,{"derivedFrom":makeQuery(id+"F1.opRevolve","SWEPT_BODY",BODY,{"disambiguationData":[OSD([sQuery(id+"F0.wireOp",EDGE,"E1")])]}),"instanceName":"1"}),"instanceName":"1"}),"instanceName":"1"}),"instanceName":"1"}),"instanceName":"1"}),"instanceName":"1"});
            var Q857;
            Q857=makeQuery(id+"F12.opPattern","COPY",BODY,{"derivedFrom":makeQuery(id+"F8.opPattern","COPY",BODY,{"derivedFrom":makeQuery(id+"F7.opPattern","COPY",BODY,{"derivedFrom":makeQuery(id+"F6.opPattern","COPY",BODY,{"derivedFrom":makeQuery(id+"F4.opPattern","COPY",BODY,{"derivedFrom":makeQuery(id+"F3.opPattern","COPY",BODY,{"derivedFrom":makeQuery(id+"F2.opPattern","COPY",BODY,{"derivedFrom":makeQuery(id+"F1.opRevolve","SWEPT_BODY",BODY,{"disambiguationData":[OSD([sQuery(id+"F0.wireOp",EDGE,"E1")])]}),"instanceName":"1"}),"instanceName":"1"}),"instanceName":"1"}),"instanceName":"1"}),"instanceName":"1"}),"instanceName":"1"}),"instanceName":"1"});
            var Q858;
            Q858=makeQuery(id+"F12.opPattern","COPY",BODY,{"derivedFrom":makeQuery(id+"F8.opPattern","COPY",BODY,{"derivedFrom":makeQuery(id+"F7.opPattern","COPY",BODY,{"derivedFrom":makeQuery(id+"F6.opPattern","COPY",BODY,{"derivedFrom":makeQuery(id+"F5.opPattern","COPY",BODY,{"derivedFrom":makeQuery(id+"F1.opRevolve","SWEPT_BODY",BODY,{"disambiguationData":[OSD([sQuery(id+"F0.wireOp",EDGE,"E1")])]}),"instanceName":"1"}),"instanceName":"1"}),"instanceName":"1"}),"instanceName":"1"}),"instanceName":"1"});
            var Q859;
            Q859=makeQuery(id+"F12.opPattern","COPY",BODY,{"derivedFrom":makeQuery(id+"F8.opPattern","COPY",BODY,{"derivedFrom":makeQuery(id+"F7.opPattern","COPY",BODY,{"derivedFrom":makeQuery(id+"F6.opPattern","COPY",BODY,{"derivedFrom":makeQuery(id+"F5.opPattern","COPY",BODY,{"derivedFrom":makeQuery(id+"F2.opPattern","COPY",BODY,{"derivedFrom":makeQuery(id+"F1.opRevolve","SWEPT_BODY",BODY,{"disambiguationData":[OSD([sQuery(id+"F0.wireOp",EDGE,"E1")])]}),"instanceName":"1"}),"instanceName":"1"}),"instanceName":"1"}),"instanceName":"1"}),"instanceName":"1"}),"instanceName":"1"});
            var Q860;
            Q860=makeQuery(id+"F12.opPattern","COPY",BODY,{"derivedFrom":makeQuery(id+"F8.opPattern","COPY",BODY,{"derivedFrom":makeQuery(id+"F7.opPattern","COPY",BODY,{"derivedFrom":makeQuery(id+"F6.opPattern","COPY",BODY,{"derivedFrom":makeQuery(id+"F5.opPattern","COPY",BODY,{"derivedFrom":makeQuery(id+"F3.opPattern","COPY",BODY,{"derivedFrom":makeQuery(id+"F2.opPattern","COPY",BODY,{"derivedFrom":makeQuery(id+"F1.opRevolve","SWEPT_BODY",BODY,{"disambiguationData":[OSD([sQuery(id+"F0.wireOp",EDGE,"E1")])]}),"instanceName":"1"}),"instanceName":"1"}),"instanceName":"1"}),"instanceName":"1"}),"instanceName":"1"}),"instanceName":"1"}),"instanceName":"1"});
            var Q861;
            Q861=makeQuery(id+"F12.opPattern","COPY",BODY,{"derivedFrom":makeQuery(id+"F8.opPattern","COPY",BODY,{"derivedFrom":makeQuery(id+"F7.opPattern","COPY",BODY,{"derivedFrom":makeQuery(id+"F6.opPattern","COPY",BODY,{"derivedFrom":makeQuery(id+"F5.opPattern","COPY",BODY,{"derivedFrom":makeQuery(id+"F4.opPattern","COPY",BODY,{"derivedFrom":makeQuery(id+"F1.opRevolve","SWEPT_BODY",BODY,{"disambiguationData":[OSD([sQuery(id+"F0.wireOp",EDGE,"E1")])]}),"instanceName":"1"}),"instanceName":"1"}),"instanceName":"1"}),"instanceName":"1"}),"instanceName":"1"}),"instanceName":"1"});
            var Q862;
            Q862=makeQuery(id+"F12.opPattern","COPY",BODY,{"derivedFrom":makeQuery(id+"F8.opPattern","COPY",BODY,{"derivedFrom":makeQuery(id+"F7.opPattern","COPY",BODY,{"derivedFrom":makeQuery(id+"F6.opPattern","COPY",BODY,{"derivedFrom":makeQuery(id+"F5.opPattern","COPY",BODY,{"derivedFrom":makeQuery(id+"F4.opPattern","COPY",BODY,{"derivedFrom":makeQuery(id+"F2.opPattern","COPY",BODY,{"derivedFrom":makeQuery(id+"F1.opRevolve","SWEPT_BODY",BODY,{"disambiguationData":[OSD([sQuery(id+"F0.wireOp",EDGE,"E1")])]}),"instanceName":"1"}),"instanceName":"1"}),"instanceName":"1"}),"instanceName":"1"}),"instanceName":"1"}),"instanceName":"1"}),"instanceName":"1"});
            var Q863;
            Q863=makeQuery(id+"F12.opPattern","COPY",BODY,{"derivedFrom":makeQuery(id+"F8.opPattern","COPY",BODY,{"derivedFrom":makeQuery(id+"F7.opPattern","COPY",BODY,{"derivedFrom":makeQuery(id+"F6.opPattern","COPY",BODY,{"derivedFrom":makeQuery(id+"F5.opPattern","COPY",BODY,{"derivedFrom":makeQuery(id+"F4.opPattern","COPY",BODY,{"derivedFrom":makeQuery(id+"F3.opPattern","COPY",BODY,{"derivedFrom":makeQuery(id+"F2.opPattern","COPY",BODY,{"derivedFrom":makeQuery(id+"F1.opRevolve","SWEPT_BODY",BODY,{"disambiguationData":[OSD([sQuery(id+"F0.wireOp",EDGE,"E1")])]}),"instanceName":"1"}),"instanceName":"1"}),"instanceName":"1"}),"instanceName":"1"}),"instanceName":"1"}),"instanceName":"1"}),"instanceName":"1"}),"instanceName":"1"});
            var Q864;
            Q864=makeQuery(id+"F12.opPattern","COPY",BODY,{"derivedFrom":makeQuery(id+"F9.opPattern","COPY",BODY,{"derivedFrom":makeQuery(id+"F1.opRevolve","SWEPT_BODY",BODY,{"disambiguationData":[OSD([sQuery(id+"F0.wireOp",EDGE,"E1")])]}),"instanceName":"1"}),"instanceName":"1"});
            var Q865;
            Q865=makeQuery(id+"F12.opPattern","COPY",BODY,{"derivedFrom":makeQuery(id+"F9.opPattern","COPY",BODY,{"derivedFrom":makeQuery(id+"F2.opPattern","COPY",BODY,{"derivedFrom":makeQuery(id+"F1.opRevolve","SWEPT_BODY",BODY,{"disambiguationData":[OSD([sQuery(id+"F0.wireOp",EDGE,"E1")])]}),"instanceName":"1"}),"instanceName":"1"}),"instanceName":"1"});
            var Q866;
            Q866=makeQuery(id+"F12.opPattern","COPY",BODY,{"derivedFrom":makeQuery(id+"F9.opPattern","COPY",BODY,{"derivedFrom":makeQuery(id+"F3.opPattern","COPY",BODY,{"derivedFrom":makeQuery(id+"F2.opPattern","COPY",BODY,{"derivedFrom":makeQuery(id+"F1.opRevolve","SWEPT_BODY",BODY,{"disambiguationData":[OSD([sQuery(id+"F0.wireOp",EDGE,"E1")])]}),"instanceName":"1"}),"instanceName":"1"}),"instanceName":"1"}),"instanceName":"1"});
            var Q867;
            Q867=makeQuery(id+"F12.opPattern","COPY",BODY,{"derivedFrom":makeQuery(id+"F9.opPattern","COPY",BODY,{"derivedFrom":makeQuery(id+"F4.opPattern","COPY",BODY,{"derivedFrom":makeQuery(id+"F1.opRevolve","SWEPT_BODY",BODY,{"disambiguationData":[OSD([sQuery(id+"F0.wireOp",EDGE,"E1")])]}),"instanceName":"1"}),"instanceName":"1"}),"instanceName":"1"});
            var Q868;
            Q868=makeQuery(id+"F12.opPattern","COPY",BODY,{"derivedFrom":makeQuery(id+"F9.opPattern","COPY",BODY,{"derivedFrom":makeQuery(id+"F4.opPattern","COPY",BODY,{"derivedFrom":makeQuery(id+"F2.opPattern","COPY",BODY,{"derivedFrom":makeQuery(id+"F1.opRevolve","SWEPT_BODY",BODY,{"disambiguationData":[OSD([sQuery(id+"F0.wireOp",EDGE,"E1")])]}),"instanceName":"1"}),"instanceName":"1"}),"instanceName":"1"}),"instanceName":"1"});
            var Q869;
            Q869=makeQuery(id+"F12.opPattern","COPY",BODY,{"derivedFrom":makeQuery(id+"F9.opPattern","COPY",BODY,{"derivedFrom":makeQuery(id+"F4.opPattern","COPY",BODY,{"derivedFrom":makeQuery(id+"F3.opPattern","COPY",BODY,{"derivedFrom":makeQuery(id+"F2.opPattern","COPY",BODY,{"derivedFrom":makeQuery(id+"F1.opRevolve","SWEPT_BODY",BODY,{"disambiguationData":[OSD([sQuery(id+"F0.wireOp",EDGE,"E1")])]}),"instanceName":"1"}),"instanceName":"1"}),"instanceName":"1"}),"instanceName":"1"}),"instanceName":"1"});
            var Q870;
            Q870=makeQuery(id+"F12.opPattern","COPY",BODY,{"derivedFrom":makeQuery(id+"F9.opPattern","COPY",BODY,{"derivedFrom":makeQuery(id+"F5.opPattern","COPY",BODY,{"derivedFrom":makeQuery(id+"F1.opRevolve","SWEPT_BODY",BODY,{"disambiguationData":[OSD([sQuery(id+"F0.wireOp",EDGE,"E1")])]}),"instanceName":"1"}),"instanceName":"1"}),"instanceName":"1"});
            var Q871;
            Q871=makeQuery(id+"F12.opPattern","COPY",BODY,{"derivedFrom":makeQuery(id+"F9.opPattern","COPY",BODY,{"derivedFrom":makeQuery(id+"F5.opPattern","COPY",BODY,{"derivedFrom":makeQuery(id+"F2.opPattern","COPY",BODY,{"derivedFrom":makeQuery(id+"F1.opRevolve","SWEPT_BODY",BODY,{"disambiguationData":[OSD([sQuery(id+"F0.wireOp",EDGE,"E1")])]}),"instanceName":"1"}),"instanceName":"1"}),"instanceName":"1"}),"instanceName":"1"});
            var Q872;
            Q872=makeQuery(id+"F12.opPattern","COPY",BODY,{"derivedFrom":makeQuery(id+"F9.opPattern","COPY",BODY,{"derivedFrom":makeQuery(id+"F5.opPattern","COPY",BODY,{"derivedFrom":makeQuery(id+"F3.opPattern","COPY",BODY,{"derivedFrom":makeQuery(id+"F2.opPattern","COPY",BODY,{"derivedFrom":makeQuery(id+"F1.opRevolve","SWEPT_BODY",BODY,{"disambiguationData":[OSD([sQuery(id+"F0.wireOp",EDGE,"E1")])]}),"instanceName":"1"}),"instanceName":"1"}),"instanceName":"1"}),"instanceName":"1"}),"instanceName":"1"});
            var Q873;
            Q873=makeQuery(id+"F12.opPattern","COPY",BODY,{"derivedFrom":makeQuery(id+"F9.opPattern","COPY",BODY,{"derivedFrom":makeQuery(id+"F5.opPattern","COPY",BODY,{"derivedFrom":makeQuery(id+"F4.opPattern","COPY",BODY,{"derivedFrom":makeQuery(id+"F1.opRevolve","SWEPT_BODY",BODY,{"disambiguationData":[OSD([sQuery(id+"F0.wireOp",EDGE,"E1")])]}),"instanceName":"1"}),"instanceName":"1"}),"instanceName":"1"}),"instanceName":"1"});
            var Q874;
            Q874=makeQuery(id+"F12.opPattern","COPY",BODY,{"derivedFrom":makeQuery(id+"F9.opPattern","COPY",BODY,{"derivedFrom":makeQuery(id+"F5.opPattern","COPY",BODY,{"derivedFrom":makeQuery(id+"F4.opPattern","COPY",BODY,{"derivedFrom":makeQuery(id+"F2.opPattern","COPY",BODY,{"derivedFrom":makeQuery(id+"F1.opRevolve","SWEPT_BODY",BODY,{"disambiguationData":[OSD([sQuery(id+"F0.wireOp",EDGE,"E1")])]}),"instanceName":"1"}),"instanceName":"1"}),"instanceName":"1"}),"instanceName":"1"}),"instanceName":"1"});
            var Q875;
            Q875=makeQuery(id+"F12.opPattern","COPY",BODY,{"derivedFrom":makeQuery(id+"F9.opPattern","COPY",BODY,{"derivedFrom":makeQuery(id+"F5.opPattern","COPY",BODY,{"derivedFrom":makeQuery(id+"F4.opPattern","COPY",BODY,{"derivedFrom":makeQuery(id+"F3.opPattern","COPY",BODY,{"derivedFrom":makeQuery(id+"F2.opPattern","COPY",BODY,{"derivedFrom":makeQuery(id+"F1.opRevolve","SWEPT_BODY",BODY,{"disambiguationData":[OSD([sQuery(id+"F0.wireOp",EDGE,"E1")])]}),"instanceName":"1"}),"instanceName":"1"}),"instanceName":"1"}),"instanceName":"1"}),"instanceName":"1"}),"instanceName":"1"});
            var Q876;
            Q876=makeQuery(id+"F12.opPattern","COPY",BODY,{"derivedFrom":makeQuery(id+"F9.opPattern","COPY",BODY,{"derivedFrom":makeQuery(id+"F6.opPattern","COPY",BODY,{"derivedFrom":makeQuery(id+"F1.opRevolve","SWEPT_BODY",BODY,{"disambiguationData":[OSD([sQuery(id+"F0.wireOp",EDGE,"E1")])]}),"instanceName":"1"}),"instanceName":"1"}),"instanceName":"1"});
            var Q877;
            Q877=makeQuery(id+"F12.opPattern","COPY",BODY,{"derivedFrom":makeQuery(id+"F9.opPattern","COPY",BODY,{"derivedFrom":makeQuery(id+"F6.opPattern","COPY",BODY,{"derivedFrom":makeQuery(id+"F2.opPattern","COPY",BODY,{"derivedFrom":makeQuery(id+"F1.opRevolve","SWEPT_BODY",BODY,{"disambiguationData":[OSD([sQuery(id+"F0.wireOp",EDGE,"E1")])]}),"instanceName":"1"}),"instanceName":"1"}),"instanceName":"1"}),"instanceName":"1"});
            var Q878;
            Q878=makeQuery(id+"F12.opPattern","COPY",BODY,{"derivedFrom":makeQuery(id+"F9.opPattern","COPY",BODY,{"derivedFrom":makeQuery(id+"F6.opPattern","COPY",BODY,{"derivedFrom":makeQuery(id+"F3.opPattern","COPY",BODY,{"derivedFrom":makeQuery(id+"F2.opPattern","COPY",BODY,{"derivedFrom":makeQuery(id+"F1.opRevolve","SWEPT_BODY",BODY,{"disambiguationData":[OSD([sQuery(id+"F0.wireOp",EDGE,"E1")])]}),"instanceName":"1"}),"instanceName":"1"}),"instanceName":"1"}),"instanceName":"1"}),"instanceName":"1"});
            var Q879;
            Q879=makeQuery(id+"F12.opPattern","COPY",BODY,{"derivedFrom":makeQuery(id+"F9.opPattern","COPY",BODY,{"derivedFrom":makeQuery(id+"F6.opPattern","COPY",BODY,{"derivedFrom":makeQuery(id+"F4.opPattern","COPY",BODY,{"derivedFrom":makeQuery(id+"F1.opRevolve","SWEPT_BODY",BODY,{"disambiguationData":[OSD([sQuery(id+"F0.wireOp",EDGE,"E1")])]}),"instanceName":"1"}),"instanceName":"1"}),"instanceName":"1"}),"instanceName":"1"});
            var Q880;
            Q880=makeQuery(id+"F12.opPattern","COPY",BODY,{"derivedFrom":makeQuery(id+"F9.opPattern","COPY",BODY,{"derivedFrom":makeQuery(id+"F6.opPattern","COPY",BODY,{"derivedFrom":makeQuery(id+"F4.opPattern","COPY",BODY,{"derivedFrom":makeQuery(id+"F2.opPattern","COPY",BODY,{"derivedFrom":makeQuery(id+"F1.opRevolve","SWEPT_BODY",BODY,{"disambiguationData":[OSD([sQuery(id+"F0.wireOp",EDGE,"E1")])]}),"instanceName":"1"}),"instanceName":"1"}),"instanceName":"1"}),"instanceName":"1"}),"instanceName":"1"});
            var Q881;
            Q881=makeQuery(id+"F12.opPattern","COPY",BODY,{"derivedFrom":makeQuery(id+"F9.opPattern","COPY",BODY,{"derivedFrom":makeQuery(id+"F6.opPattern","COPY",BODY,{"derivedFrom":makeQuery(id+"F4.opPattern","COPY",BODY,{"derivedFrom":makeQuery(id+"F3.opPattern","COPY",BODY,{"derivedFrom":makeQuery(id+"F2.opPattern","COPY",BODY,{"derivedFrom":makeQuery(id+"F1.opRevolve","SWEPT_BODY",BODY,{"disambiguationData":[OSD([sQuery(id+"F0.wireOp",EDGE,"E1")])]}),"instanceName":"1"}),"instanceName":"1"}),"instanceName":"1"}),"instanceName":"1"}),"instanceName":"1"}),"instanceName":"1"});
            var Q882;
            Q882=makeQuery(id+"F12.opPattern","COPY",BODY,{"derivedFrom":makeQuery(id+"F9.opPattern","COPY",BODY,{"derivedFrom":makeQuery(id+"F6.opPattern","COPY",BODY,{"derivedFrom":makeQuery(id+"F5.opPattern","COPY",BODY,{"derivedFrom":makeQuery(id+"F1.opRevolve","SWEPT_BODY",BODY,{"disambiguationData":[OSD([sQuery(id+"F0.wireOp",EDGE,"E1")])]}),"instanceName":"1"}),"instanceName":"1"}),"instanceName":"1"}),"instanceName":"1"});
            var Q883;
            Q883=makeQuery(id+"F12.opPattern","COPY",BODY,{"derivedFrom":makeQuery(id+"F9.opPattern","COPY",BODY,{"derivedFrom":makeQuery(id+"F6.opPattern","COPY",BODY,{"derivedFrom":makeQuery(id+"F5.opPattern","COPY",BODY,{"derivedFrom":makeQuery(id+"F2.opPattern","COPY",BODY,{"derivedFrom":makeQuery(id+"F1.opRevolve","SWEPT_BODY",BODY,{"disambiguationData":[OSD([sQuery(id+"F0.wireOp",EDGE,"E1")])]}),"instanceName":"1"}),"instanceName":"1"}),"instanceName":"1"}),"instanceName":"1"}),"instanceName":"1"});
            var Q884;
            Q884=makeQuery(id+"F12.opPattern","COPY",BODY,{"derivedFrom":makeQuery(id+"F9.opPattern","COPY",BODY,{"derivedFrom":makeQuery(id+"F6.opPattern","COPY",BODY,{"derivedFrom":makeQuery(id+"F5.opPattern","COPY",BODY,{"derivedFrom":makeQuery(id+"F3.opPattern","COPY",BODY,{"derivedFrom":makeQuery(id+"F2.opPattern","COPY",BODY,{"derivedFrom":makeQuery(id+"F1.opRevolve","SWEPT_BODY",BODY,{"disambiguationData":[OSD([sQuery(id+"F0.wireOp",EDGE,"E1")])]}),"instanceName":"1"}),"instanceName":"1"}),"instanceName":"1"}),"instanceName":"1"}),"instanceName":"1"}),"instanceName":"1"});
            var Q885;
            Q885=makeQuery(id+"F12.opPattern","COPY",BODY,{"derivedFrom":makeQuery(id+"F9.opPattern","COPY",BODY,{"derivedFrom":makeQuery(id+"F6.opPattern","COPY",BODY,{"derivedFrom":makeQuery(id+"F5.opPattern","COPY",BODY,{"derivedFrom":makeQuery(id+"F4.opPattern","COPY",BODY,{"derivedFrom":makeQuery(id+"F1.opRevolve","SWEPT_BODY",BODY,{"disambiguationData":[OSD([sQuery(id+"F0.wireOp",EDGE,"E1")])]}),"instanceName":"1"}),"instanceName":"1"}),"instanceName":"1"}),"instanceName":"1"}),"instanceName":"1"});
            var Q886;
            Q886=makeQuery(id+"F12.opPattern","COPY",BODY,{"derivedFrom":makeQuery(id+"F9.opPattern","COPY",BODY,{"derivedFrom":makeQuery(id+"F6.opPattern","COPY",BODY,{"derivedFrom":makeQuery(id+"F5.opPattern","COPY",BODY,{"derivedFrom":makeQuery(id+"F4.opPattern","COPY",BODY,{"derivedFrom":makeQuery(id+"F2.opPattern","COPY",BODY,{"derivedFrom":makeQuery(id+"F1.opRevolve","SWEPT_BODY",BODY,{"disambiguationData":[OSD([sQuery(id+"F0.wireOp",EDGE,"E1")])]}),"instanceName":"1"}),"instanceName":"1"}),"instanceName":"1"}),"instanceName":"1"}),"instanceName":"1"}),"instanceName":"1"});
            var Q887;
            Q887=makeQuery(id+"F12.opPattern","COPY",BODY,{"derivedFrom":makeQuery(id+"F9.opPattern","COPY",BODY,{"derivedFrom":makeQuery(id+"F6.opPattern","COPY",BODY,{"derivedFrom":makeQuery(id+"F5.opPattern","COPY",BODY,{"derivedFrom":makeQuery(id+"F4.opPattern","COPY",BODY,{"derivedFrom":makeQuery(id+"F3.opPattern","COPY",BODY,{"derivedFrom":makeQuery(id+"F2.opPattern","COPY",BODY,{"derivedFrom":makeQuery(id+"F1.opRevolve","SWEPT_BODY",BODY,{"disambiguationData":[OSD([sQuery(id+"F0.wireOp",EDGE,"E1")])]}),"instanceName":"1"}),"instanceName":"1"}),"instanceName":"1"}),"instanceName":"1"}),"instanceName":"1"}),"instanceName":"1"}),"instanceName":"1"});
            var Q888;
            Q888=makeQuery(id+"F12.opPattern","COPY",BODY,{"derivedFrom":makeQuery(id+"F9.opPattern","COPY",BODY,{"derivedFrom":makeQuery(id+"F7.opPattern","COPY",BODY,{"derivedFrom":makeQuery(id+"F1.opRevolve","SWEPT_BODY",BODY,{"disambiguationData":[OSD([sQuery(id+"F0.wireOp",EDGE,"E1")])]}),"instanceName":"1"}),"instanceName":"1"}),"instanceName":"1"});
            var Q889;
            Q889=makeQuery(id+"F12.opPattern","COPY",BODY,{"derivedFrom":makeQuery(id+"F9.opPattern","COPY",BODY,{"derivedFrom":makeQuery(id+"F7.opPattern","COPY",BODY,{"derivedFrom":makeQuery(id+"F2.opPattern","COPY",BODY,{"derivedFrom":makeQuery(id+"F1.opRevolve","SWEPT_BODY",BODY,{"disambiguationData":[OSD([sQuery(id+"F0.wireOp",EDGE,"E1")])]}),"instanceName":"1"}),"instanceName":"1"}),"instanceName":"1"}),"instanceName":"1"});
            var Q890;
            Q890=makeQuery(id+"F12.opPattern","COPY",BODY,{"derivedFrom":makeQuery(id+"F9.opPattern","COPY",BODY,{"derivedFrom":makeQuery(id+"F7.opPattern","COPY",BODY,{"derivedFrom":makeQuery(id+"F3.opPattern","COPY",BODY,{"derivedFrom":makeQuery(id+"F2.opPattern","COPY",BODY,{"derivedFrom":makeQuery(id+"F1.opRevolve","SWEPT_BODY",BODY,{"disambiguationData":[OSD([sQuery(id+"F0.wireOp",EDGE,"E1")])]}),"instanceName":"1"}),"instanceName":"1"}),"instanceName":"1"}),"instanceName":"1"}),"instanceName":"1"});
            var Q891;
            Q891=makeQuery(id+"F12.opPattern","COPY",BODY,{"derivedFrom":makeQuery(id+"F9.opPattern","COPY",BODY,{"derivedFrom":makeQuery(id+"F7.opPattern","COPY",BODY,{"derivedFrom":makeQuery(id+"F4.opPattern","COPY",BODY,{"derivedFrom":makeQuery(id+"F1.opRevolve","SWEPT_BODY",BODY,{"disambiguationData":[OSD([sQuery(id+"F0.wireOp",EDGE,"E1")])]}),"instanceName":"1"}),"instanceName":"1"}),"instanceName":"1"}),"instanceName":"1"});
            var Q892;
            Q892=makeQuery(id+"F12.opPattern","COPY",BODY,{"derivedFrom":makeQuery(id+"F9.opPattern","COPY",BODY,{"derivedFrom":makeQuery(id+"F7.opPattern","COPY",BODY,{"derivedFrom":makeQuery(id+"F4.opPattern","COPY",BODY,{"derivedFrom":makeQuery(id+"F2.opPattern","COPY",BODY,{"derivedFrom":makeQuery(id+"F1.opRevolve","SWEPT_BODY",BODY,{"disambiguationData":[OSD([sQuery(id+"F0.wireOp",EDGE,"E1")])]}),"instanceName":"1"}),"instanceName":"1"}),"instanceName":"1"}),"instanceName":"1"}),"instanceName":"1"});
            var Q893;
            Q893=makeQuery(id+"F12.opPattern","COPY",BODY,{"derivedFrom":makeQuery(id+"F9.opPattern","COPY",BODY,{"derivedFrom":makeQuery(id+"F7.opPattern","COPY",BODY,{"derivedFrom":makeQuery(id+"F4.opPattern","COPY",BODY,{"derivedFrom":makeQuery(id+"F3.opPattern","COPY",BODY,{"derivedFrom":makeQuery(id+"F2.opPattern","COPY",BODY,{"derivedFrom":makeQuery(id+"F1.opRevolve","SWEPT_BODY",BODY,{"disambiguationData":[OSD([sQuery(id+"F0.wireOp",EDGE,"E1")])]}),"instanceName":"1"}),"instanceName":"1"}),"instanceName":"1"}),"instanceName":"1"}),"instanceName":"1"}),"instanceName":"1"});
            var Q894;
            Q894=makeQuery(id+"F12.opPattern","COPY",BODY,{"derivedFrom":makeQuery(id+"F9.opPattern","COPY",BODY,{"derivedFrom":makeQuery(id+"F7.opPattern","COPY",BODY,{"derivedFrom":makeQuery(id+"F5.opPattern","COPY",BODY,{"derivedFrom":makeQuery(id+"F1.opRevolve","SWEPT_BODY",BODY,{"disambiguationData":[OSD([sQuery(id+"F0.wireOp",EDGE,"E1")])]}),"instanceName":"1"}),"instanceName":"1"}),"instanceName":"1"}),"instanceName":"1"});
            var Q895;
            Q895=makeQuery(id+"F12.opPattern","COPY",BODY,{"derivedFrom":makeQuery(id+"F9.opPattern","COPY",BODY,{"derivedFrom":makeQuery(id+"F7.opPattern","COPY",BODY,{"derivedFrom":makeQuery(id+"F5.opPattern","COPY",BODY,{"derivedFrom":makeQuery(id+"F2.opPattern","COPY",BODY,{"derivedFrom":makeQuery(id+"F1.opRevolve","SWEPT_BODY",BODY,{"disambiguationData":[OSD([sQuery(id+"F0.wireOp",EDGE,"E1")])]}),"instanceName":"1"}),"instanceName":"1"}),"instanceName":"1"}),"instanceName":"1"}),"instanceName":"1"});
            var Q896;
            Q896=makeQuery(id+"F12.opPattern","COPY",BODY,{"derivedFrom":makeQuery(id+"F9.opPattern","COPY",BODY,{"derivedFrom":makeQuery(id+"F7.opPattern","COPY",BODY,{"derivedFrom":makeQuery(id+"F5.opPattern","COPY",BODY,{"derivedFrom":makeQuery(id+"F3.opPattern","COPY",BODY,{"derivedFrom":makeQuery(id+"F2.opPattern","COPY",BODY,{"derivedFrom":makeQuery(id+"F1.opRevolve","SWEPT_BODY",BODY,{"disambiguationData":[OSD([sQuery(id+"F0.wireOp",EDGE,"E1")])]}),"instanceName":"1"}),"instanceName":"1"}),"instanceName":"1"}),"instanceName":"1"}),"instanceName":"1"}),"instanceName":"1"});
            var Q897;
            Q897=makeQuery(id+"F12.opPattern","COPY",BODY,{"derivedFrom":makeQuery(id+"F9.opPattern","COPY",BODY,{"derivedFrom":makeQuery(id+"F7.opPattern","COPY",BODY,{"derivedFrom":makeQuery(id+"F5.opPattern","COPY",BODY,{"derivedFrom":makeQuery(id+"F4.opPattern","COPY",BODY,{"derivedFrom":makeQuery(id+"F1.opRevolve","SWEPT_BODY",BODY,{"disambiguationData":[OSD([sQuery(id+"F0.wireOp",EDGE,"E1")])]}),"instanceName":"1"}),"instanceName":"1"}),"instanceName":"1"}),"instanceName":"1"}),"instanceName":"1"});
            var Q898;
            Q898=makeQuery(id+"F12.opPattern","COPY",BODY,{"derivedFrom":makeQuery(id+"F9.opPattern","COPY",BODY,{"derivedFrom":makeQuery(id+"F7.opPattern","COPY",BODY,{"derivedFrom":makeQuery(id+"F5.opPattern","COPY",BODY,{"derivedFrom":makeQuery(id+"F4.opPattern","COPY",BODY,{"derivedFrom":makeQuery(id+"F2.opPattern","COPY",BODY,{"derivedFrom":makeQuery(id+"F1.opRevolve","SWEPT_BODY",BODY,{"disambiguationData":[OSD([sQuery(id+"F0.wireOp",EDGE,"E1")])]}),"instanceName":"1"}),"instanceName":"1"}),"instanceName":"1"}),"instanceName":"1"}),"instanceName":"1"}),"instanceName":"1"});
            var Q899;
            Q899=makeQuery(id+"F12.opPattern","COPY",BODY,{"derivedFrom":makeQuery(id+"F9.opPattern","COPY",BODY,{"derivedFrom":makeQuery(id+"F7.opPattern","COPY",BODY,{"derivedFrom":makeQuery(id+"F5.opPattern","COPY",BODY,{"derivedFrom":makeQuery(id+"F4.opPattern","COPY",BODY,{"derivedFrom":makeQuery(id+"F3.opPattern","COPY",BODY,{"derivedFrom":makeQuery(id+"F2.opPattern","COPY",BODY,{"derivedFrom":makeQuery(id+"F1.opRevolve","SWEPT_BODY",BODY,{"disambiguationData":[OSD([sQuery(id+"F0.wireOp",EDGE,"E1")])]}),"instanceName":"1"}),"instanceName":"1"}),"instanceName":"1"}),"instanceName":"1"}),"instanceName":"1"}),"instanceName":"1"}),"instanceName":"1"});
            var Q900;
            Q900=makeQuery(id+"F12.opPattern","COPY",BODY,{"derivedFrom":makeQuery(id+"F9.opPattern","COPY",BODY,{"derivedFrom":makeQuery(id+"F7.opPattern","COPY",BODY,{"derivedFrom":makeQuery(id+"F6.opPattern","COPY",BODY,{"derivedFrom":makeQuery(id+"F1.opRevolve","SWEPT_BODY",BODY,{"disambiguationData":[OSD([sQuery(id+"F0.wireOp",EDGE,"E1")])]}),"instanceName":"1"}),"instanceName":"1"}),"instanceName":"1"}),"instanceName":"1"});
            var Q901;
            Q901=makeQuery(id+"F12.opPattern","COPY",BODY,{"derivedFrom":makeQuery(id+"F9.opPattern","COPY",BODY,{"derivedFrom":makeQuery(id+"F7.opPattern","COPY",BODY,{"derivedFrom":makeQuery(id+"F6.opPattern","COPY",BODY,{"derivedFrom":makeQuery(id+"F2.opPattern","COPY",BODY,{"derivedFrom":makeQuery(id+"F1.opRevolve","SWEPT_BODY",BODY,{"disambiguationData":[OSD([sQuery(id+"F0.wireOp",EDGE,"E1")])]}),"instanceName":"1"}),"instanceName":"1"}),"instanceName":"1"}),"instanceName":"1"}),"instanceName":"1"});
            var Q902;
            Q902=makeQuery(id+"F12.opPattern","COPY",BODY,{"derivedFrom":makeQuery(id+"F9.opPattern","COPY",BODY,{"derivedFrom":makeQuery(id+"F7.opPattern","COPY",BODY,{"derivedFrom":makeQuery(id+"F6.opPattern","COPY",BODY,{"derivedFrom":makeQuery(id+"F3.opPattern","COPY",BODY,{"derivedFrom":makeQuery(id+"F2.opPattern","COPY",BODY,{"derivedFrom":makeQuery(id+"F1.opRevolve","SWEPT_BODY",BODY,{"disambiguationData":[OSD([sQuery(id+"F0.wireOp",EDGE,"E1")])]}),"instanceName":"1"}),"instanceName":"1"}),"instanceName":"1"}),"instanceName":"1"}),"instanceName":"1"}),"instanceName":"1"});
            var Q903;
            Q903=makeQuery(id+"F12.opPattern","COPY",BODY,{"derivedFrom":makeQuery(id+"F9.opPattern","COPY",BODY,{"derivedFrom":makeQuery(id+"F7.opPattern","COPY",BODY,{"derivedFrom":makeQuery(id+"F6.opPattern","COPY",BODY,{"derivedFrom":makeQuery(id+"F4.opPattern","COPY",BODY,{"derivedFrom":makeQuery(id+"F1.opRevolve","SWEPT_BODY",BODY,{"disambiguationData":[OSD([sQuery(id+"F0.wireOp",EDGE,"E1")])]}),"instanceName":"1"}),"instanceName":"1"}),"instanceName":"1"}),"instanceName":"1"}),"instanceName":"1"});
            var Q904;
            Q904=makeQuery(id+"F12.opPattern","COPY",BODY,{"derivedFrom":makeQuery(id+"F9.opPattern","COPY",BODY,{"derivedFrom":makeQuery(id+"F7.opPattern","COPY",BODY,{"derivedFrom":makeQuery(id+"F6.opPattern","COPY",BODY,{"derivedFrom":makeQuery(id+"F4.opPattern","COPY",BODY,{"derivedFrom":makeQuery(id+"F2.opPattern","COPY",BODY,{"derivedFrom":makeQuery(id+"F1.opRevolve","SWEPT_BODY",BODY,{"disambiguationData":[OSD([sQuery(id+"F0.wireOp",EDGE,"E1")])]}),"instanceName":"1"}),"instanceName":"1"}),"instanceName":"1"}),"instanceName":"1"}),"instanceName":"1"}),"instanceName":"1"});
            var Q905;
            Q905=makeQuery(id+"F12.opPattern","COPY",BODY,{"derivedFrom":makeQuery(id+"F9.opPattern","COPY",BODY,{"derivedFrom":makeQuery(id+"F7.opPattern","COPY",BODY,{"derivedFrom":makeQuery(id+"F6.opPattern","COPY",BODY,{"derivedFrom":makeQuery(id+"F4.opPattern","COPY",BODY,{"derivedFrom":makeQuery(id+"F3.opPattern","COPY",BODY,{"derivedFrom":makeQuery(id+"F2.opPattern","COPY",BODY,{"derivedFrom":makeQuery(id+"F1.opRevolve","SWEPT_BODY",BODY,{"disambiguationData":[OSD([sQuery(id+"F0.wireOp",EDGE,"E1")])]}),"instanceName":"1"}),"instanceName":"1"}),"instanceName":"1"}),"instanceName":"1"}),"instanceName":"1"}),"instanceName":"1"}),"instanceName":"1"});
            var Q906;
            Q906=makeQuery(id+"F12.opPattern","COPY",BODY,{"derivedFrom":makeQuery(id+"F9.opPattern","COPY",BODY,{"derivedFrom":makeQuery(id+"F7.opPattern","COPY",BODY,{"derivedFrom":makeQuery(id+"F6.opPattern","COPY",BODY,{"derivedFrom":makeQuery(id+"F5.opPattern","COPY",BODY,{"derivedFrom":makeQuery(id+"F1.opRevolve","SWEPT_BODY",BODY,{"disambiguationData":[OSD([sQuery(id+"F0.wireOp",EDGE,"E1")])]}),"instanceName":"1"}),"instanceName":"1"}),"instanceName":"1"}),"instanceName":"1"}),"instanceName":"1"});
            var Q907;
            Q907=makeQuery(id+"F12.opPattern","COPY",BODY,{"derivedFrom":makeQuery(id+"F9.opPattern","COPY",BODY,{"derivedFrom":makeQuery(id+"F7.opPattern","COPY",BODY,{"derivedFrom":makeQuery(id+"F6.opPattern","COPY",BODY,{"derivedFrom":makeQuery(id+"F5.opPattern","COPY",BODY,{"derivedFrom":makeQuery(id+"F2.opPattern","COPY",BODY,{"derivedFrom":makeQuery(id+"F1.opRevolve","SWEPT_BODY",BODY,{"disambiguationData":[OSD([sQuery(id+"F0.wireOp",EDGE,"E1")])]}),"instanceName":"1"}),"instanceName":"1"}),"instanceName":"1"}),"instanceName":"1"}),"instanceName":"1"}),"instanceName":"1"});
            var Q908;
            Q908=makeQuery(id+"F12.opPattern","COPY",BODY,{"derivedFrom":makeQuery(id+"F9.opPattern","COPY",BODY,{"derivedFrom":makeQuery(id+"F7.opPattern","COPY",BODY,{"derivedFrom":makeQuery(id+"F6.opPattern","COPY",BODY,{"derivedFrom":makeQuery(id+"F5.opPattern","COPY",BODY,{"derivedFrom":makeQuery(id+"F3.opPattern","COPY",BODY,{"derivedFrom":makeQuery(id+"F2.opPattern","COPY",BODY,{"derivedFrom":makeQuery(id+"F1.opRevolve","SWEPT_BODY",BODY,{"disambiguationData":[OSD([sQuery(id+"F0.wireOp",EDGE,"E1")])]}),"instanceName":"1"}),"instanceName":"1"}),"instanceName":"1"}),"instanceName":"1"}),"instanceName":"1"}),"instanceName":"1"}),"instanceName":"1"});
            var Q909;
            Q909=makeQuery(id+"F12.opPattern","COPY",BODY,{"derivedFrom":makeQuery(id+"F9.opPattern","COPY",BODY,{"derivedFrom":makeQuery(id+"F7.opPattern","COPY",BODY,{"derivedFrom":makeQuery(id+"F6.opPattern","COPY",BODY,{"derivedFrom":makeQuery(id+"F5.opPattern","COPY",BODY,{"derivedFrom":makeQuery(id+"F4.opPattern","COPY",BODY,{"derivedFrom":makeQuery(id+"F1.opRevolve","SWEPT_BODY",BODY,{"disambiguationData":[OSD([sQuery(id+"F0.wireOp",EDGE,"E1")])]}),"instanceName":"1"}),"instanceName":"1"}),"instanceName":"1"}),"instanceName":"1"}),"instanceName":"1"}),"instanceName":"1"});
            var Q910;
            Q910=makeQuery(id+"F12.opPattern","COPY",BODY,{"derivedFrom":makeQuery(id+"F9.opPattern","COPY",BODY,{"derivedFrom":makeQuery(id+"F7.opPattern","COPY",BODY,{"derivedFrom":makeQuery(id+"F6.opPattern","COPY",BODY,{"derivedFrom":makeQuery(id+"F5.opPattern","COPY",BODY,{"derivedFrom":makeQuery(id+"F4.opPattern","COPY",BODY,{"derivedFrom":makeQuery(id+"F2.opPattern","COPY",BODY,{"derivedFrom":makeQuery(id+"F1.opRevolve","SWEPT_BODY",BODY,{"disambiguationData":[OSD([sQuery(id+"F0.wireOp",EDGE,"E1")])]}),"instanceName":"1"}),"instanceName":"1"}),"instanceName":"1"}),"instanceName":"1"}),"instanceName":"1"}),"instanceName":"1"}),"instanceName":"1"});
            var Q911;
            Q911=makeQuery(id+"F12.opPattern","COPY",BODY,{"derivedFrom":makeQuery(id+"F9.opPattern","COPY",BODY,{"derivedFrom":makeQuery(id+"F7.opPattern","COPY",BODY,{"derivedFrom":makeQuery(id+"F6.opPattern","COPY",BODY,{"derivedFrom":makeQuery(id+"F5.opPattern","COPY",BODY,{"derivedFrom":makeQuery(id+"F4.opPattern","COPY",BODY,{"derivedFrom":makeQuery(id+"F3.opPattern","COPY",BODY,{"derivedFrom":makeQuery(id+"F2.opPattern","COPY",BODY,{"derivedFrom":makeQuery(id+"F1.opRevolve","SWEPT_BODY",BODY,{"disambiguationData":[OSD([sQuery(id+"F0.wireOp",EDGE,"E1")])]}),"instanceName":"1"}),"instanceName":"1"}),"instanceName":"1"}),"instanceName":"1"}),"instanceName":"1"}),"instanceName":"1"}),"instanceName":"1"}),"instanceName":"1"});
            var Q912;
            Q912=makeQuery(id+"F12.opPattern","COPY",BODY,{"derivedFrom":makeQuery(id+"F9.opPattern","COPY",BODY,{"derivedFrom":makeQuery(id+"F8.opPattern","COPY",BODY,{"derivedFrom":makeQuery(id+"F1.opRevolve","SWEPT_BODY",BODY,{"disambiguationData":[OSD([sQuery(id+"F0.wireOp",EDGE,"E1")])]}),"instanceName":"1"}),"instanceName":"1"}),"instanceName":"1"});
            var Q913;
            Q913=makeQuery(id+"F12.opPattern","COPY",BODY,{"derivedFrom":makeQuery(id+"F9.opPattern","COPY",BODY,{"derivedFrom":makeQuery(id+"F8.opPattern","COPY",BODY,{"derivedFrom":makeQuery(id+"F2.opPattern","COPY",BODY,{"derivedFrom":makeQuery(id+"F1.opRevolve","SWEPT_BODY",BODY,{"disambiguationData":[OSD([sQuery(id+"F0.wireOp",EDGE,"E1")])]}),"instanceName":"1"}),"instanceName":"1"}),"instanceName":"1"}),"instanceName":"1"});
            var Q914;
            Q914=makeQuery(id+"F12.opPattern","COPY",BODY,{"derivedFrom":makeQuery(id+"F9.opPattern","COPY",BODY,{"derivedFrom":makeQuery(id+"F8.opPattern","COPY",BODY,{"derivedFrom":makeQuery(id+"F3.opPattern","COPY",BODY,{"derivedFrom":makeQuery(id+"F2.opPattern","COPY",BODY,{"derivedFrom":makeQuery(id+"F1.opRevolve","SWEPT_BODY",BODY,{"disambiguationData":[OSD([sQuery(id+"F0.wireOp",EDGE,"E1")])]}),"instanceName":"1"}),"instanceName":"1"}),"instanceName":"1"}),"instanceName":"1"}),"instanceName":"1"});
            var Q915;
            Q915=makeQuery(id+"F12.opPattern","COPY",BODY,{"derivedFrom":makeQuery(id+"F9.opPattern","COPY",BODY,{"derivedFrom":makeQuery(id+"F8.opPattern","COPY",BODY,{"derivedFrom":makeQuery(id+"F4.opPattern","COPY",BODY,{"derivedFrom":makeQuery(id+"F1.opRevolve","SWEPT_BODY",BODY,{"disambiguationData":[OSD([sQuery(id+"F0.wireOp",EDGE,"E1")])]}),"instanceName":"1"}),"instanceName":"1"}),"instanceName":"1"}),"instanceName":"1"});
            var Q916;
            Q916=makeQuery(id+"F12.opPattern","COPY",BODY,{"derivedFrom":makeQuery(id+"F9.opPattern","COPY",BODY,{"derivedFrom":makeQuery(id+"F8.opPattern","COPY",BODY,{"derivedFrom":makeQuery(id+"F4.opPattern","COPY",BODY,{"derivedFrom":makeQuery(id+"F2.opPattern","COPY",BODY,{"derivedFrom":makeQuery(id+"F1.opRevolve","SWEPT_BODY",BODY,{"disambiguationData":[OSD([sQuery(id+"F0.wireOp",EDGE,"E1")])]}),"instanceName":"1"}),"instanceName":"1"}),"instanceName":"1"}),"instanceName":"1"}),"instanceName":"1"});
            var Q917;
            Q917=makeQuery(id+"F12.opPattern","COPY",BODY,{"derivedFrom":makeQuery(id+"F9.opPattern","COPY",BODY,{"derivedFrom":makeQuery(id+"F8.opPattern","COPY",BODY,{"derivedFrom":makeQuery(id+"F4.opPattern","COPY",BODY,{"derivedFrom":makeQuery(id+"F3.opPattern","COPY",BODY,{"derivedFrom":makeQuery(id+"F2.opPattern","COPY",BODY,{"derivedFrom":makeQuery(id+"F1.opRevolve","SWEPT_BODY",BODY,{"disambiguationData":[OSD([sQuery(id+"F0.wireOp",EDGE,"E1")])]}),"instanceName":"1"}),"instanceName":"1"}),"instanceName":"1"}),"instanceName":"1"}),"instanceName":"1"}),"instanceName":"1"});
            var Q918;
            Q918=makeQuery(id+"F12.opPattern","COPY",BODY,{"derivedFrom":makeQuery(id+"F9.opPattern","COPY",BODY,{"derivedFrom":makeQuery(id+"F8.opPattern","COPY",BODY,{"derivedFrom":makeQuery(id+"F5.opPattern","COPY",BODY,{"derivedFrom":makeQuery(id+"F1.opRevolve","SWEPT_BODY",BODY,{"disambiguationData":[OSD([sQuery(id+"F0.wireOp",EDGE,"E1")])]}),"instanceName":"1"}),"instanceName":"1"}),"instanceName":"1"}),"instanceName":"1"});
            var Q919;
            Q919=makeQuery(id+"F12.opPattern","COPY",BODY,{"derivedFrom":makeQuery(id+"F9.opPattern","COPY",BODY,{"derivedFrom":makeQuery(id+"F8.opPattern","COPY",BODY,{"derivedFrom":makeQuery(id+"F5.opPattern","COPY",BODY,{"derivedFrom":makeQuery(id+"F2.opPattern","COPY",BODY,{"derivedFrom":makeQuery(id+"F1.opRevolve","SWEPT_BODY",BODY,{"disambiguationData":[OSD([sQuery(id+"F0.wireOp",EDGE,"E1")])]}),"instanceName":"1"}),"instanceName":"1"}),"instanceName":"1"}),"instanceName":"1"}),"instanceName":"1"});
            var Q920;
            Q920=makeQuery(id+"F12.opPattern","COPY",BODY,{"derivedFrom":makeQuery(id+"F9.opPattern","COPY",BODY,{"derivedFrom":makeQuery(id+"F8.opPattern","COPY",BODY,{"derivedFrom":makeQuery(id+"F5.opPattern","COPY",BODY,{"derivedFrom":makeQuery(id+"F3.opPattern","COPY",BODY,{"derivedFrom":makeQuery(id+"F2.opPattern","COPY",BODY,{"derivedFrom":makeQuery(id+"F1.opRevolve","SWEPT_BODY",BODY,{"disambiguationData":[OSD([sQuery(id+"F0.wireOp",EDGE,"E1")])]}),"instanceName":"1"}),"instanceName":"1"}),"instanceName":"1"}),"instanceName":"1"}),"instanceName":"1"}),"instanceName":"1"});
            var Q921;
            Q921=makeQuery(id+"F12.opPattern","COPY",BODY,{"derivedFrom":makeQuery(id+"F9.opPattern","COPY",BODY,{"derivedFrom":makeQuery(id+"F8.opPattern","COPY",BODY,{"derivedFrom":makeQuery(id+"F5.opPattern","COPY",BODY,{"derivedFrom":makeQuery(id+"F4.opPattern","COPY",BODY,{"derivedFrom":makeQuery(id+"F1.opRevolve","SWEPT_BODY",BODY,{"disambiguationData":[OSD([sQuery(id+"F0.wireOp",EDGE,"E1")])]}),"instanceName":"1"}),"instanceName":"1"}),"instanceName":"1"}),"instanceName":"1"}),"instanceName":"1"});
            var Q922;
            Q922=makeQuery(id+"F12.opPattern","COPY",BODY,{"derivedFrom":makeQuery(id+"F9.opPattern","COPY",BODY,{"derivedFrom":makeQuery(id+"F8.opPattern","COPY",BODY,{"derivedFrom":makeQuery(id+"F5.opPattern","COPY",BODY,{"derivedFrom":makeQuery(id+"F4.opPattern","COPY",BODY,{"derivedFrom":makeQuery(id+"F2.opPattern","COPY",BODY,{"derivedFrom":makeQuery(id+"F1.opRevolve","SWEPT_BODY",BODY,{"disambiguationData":[OSD([sQuery(id+"F0.wireOp",EDGE,"E1")])]}),"instanceName":"1"}),"instanceName":"1"}),"instanceName":"1"}),"instanceName":"1"}),"instanceName":"1"}),"instanceName":"1"});
            var Q923;
            Q923=makeQuery(id+"F12.opPattern","COPY",BODY,{"derivedFrom":makeQuery(id+"F9.opPattern","COPY",BODY,{"derivedFrom":makeQuery(id+"F8.opPattern","COPY",BODY,{"derivedFrom":makeQuery(id+"F5.opPattern","COPY",BODY,{"derivedFrom":makeQuery(id+"F4.opPattern","COPY",BODY,{"derivedFrom":makeQuery(id+"F3.opPattern","COPY",BODY,{"derivedFrom":makeQuery(id+"F2.opPattern","COPY",BODY,{"derivedFrom":makeQuery(id+"F1.opRevolve","SWEPT_BODY",BODY,{"disambiguationData":[OSD([sQuery(id+"F0.wireOp",EDGE,"E1")])]}),"instanceName":"1"}),"instanceName":"1"}),"instanceName":"1"}),"instanceName":"1"}),"instanceName":"1"}),"instanceName":"1"}),"instanceName":"1"});
            var Q924;
            Q924=makeQuery(id+"F12.opPattern","COPY",BODY,{"derivedFrom":makeQuery(id+"F9.opPattern","COPY",BODY,{"derivedFrom":makeQuery(id+"F8.opPattern","COPY",BODY,{"derivedFrom":makeQuery(id+"F6.opPattern","COPY",BODY,{"derivedFrom":makeQuery(id+"F1.opRevolve","SWEPT_BODY",BODY,{"disambiguationData":[OSD([sQuery(id+"F0.wireOp",EDGE,"E1")])]}),"instanceName":"1"}),"instanceName":"1"}),"instanceName":"1"}),"instanceName":"1"});
            var Q925;
            Q925=makeQuery(id+"F12.opPattern","COPY",BODY,{"derivedFrom":makeQuery(id+"F9.opPattern","COPY",BODY,{"derivedFrom":makeQuery(id+"F8.opPattern","COPY",BODY,{"derivedFrom":makeQuery(id+"F6.opPattern","COPY",BODY,{"derivedFrom":makeQuery(id+"F2.opPattern","COPY",BODY,{"derivedFrom":makeQuery(id+"F1.opRevolve","SWEPT_BODY",BODY,{"disambiguationData":[OSD([sQuery(id+"F0.wireOp",EDGE,"E1")])]}),"instanceName":"1"}),"instanceName":"1"}),"instanceName":"1"}),"instanceName":"1"}),"instanceName":"1"});
            var Q926;
            Q926=makeQuery(id+"F12.opPattern","COPY",BODY,{"derivedFrom":makeQuery(id+"F9.opPattern","COPY",BODY,{"derivedFrom":makeQuery(id+"F8.opPattern","COPY",BODY,{"derivedFrom":makeQuery(id+"F6.opPattern","COPY",BODY,{"derivedFrom":makeQuery(id+"F3.opPattern","COPY",BODY,{"derivedFrom":makeQuery(id+"F2.opPattern","COPY",BODY,{"derivedFrom":makeQuery(id+"F1.opRevolve","SWEPT_BODY",BODY,{"disambiguationData":[OSD([sQuery(id+"F0.wireOp",EDGE,"E1")])]}),"instanceName":"1"}),"instanceName":"1"}),"instanceName":"1"}),"instanceName":"1"}),"instanceName":"1"}),"instanceName":"1"});
            var Q927;
            Q927=makeQuery(id+"F12.opPattern","COPY",BODY,{"derivedFrom":makeQuery(id+"F9.opPattern","COPY",BODY,{"derivedFrom":makeQuery(id+"F8.opPattern","COPY",BODY,{"derivedFrom":makeQuery(id+"F6.opPattern","COPY",BODY,{"derivedFrom":makeQuery(id+"F4.opPattern","COPY",BODY,{"derivedFrom":makeQuery(id+"F1.opRevolve","SWEPT_BODY",BODY,{"disambiguationData":[OSD([sQuery(id+"F0.wireOp",EDGE,"E1")])]}),"instanceName":"1"}),"instanceName":"1"}),"instanceName":"1"}),"instanceName":"1"}),"instanceName":"1"});
            var Q928;
            Q928=makeQuery(id+"F12.opPattern","COPY",BODY,{"derivedFrom":makeQuery(id+"F9.opPattern","COPY",BODY,{"derivedFrom":makeQuery(id+"F8.opPattern","COPY",BODY,{"derivedFrom":makeQuery(id+"F6.opPattern","COPY",BODY,{"derivedFrom":makeQuery(id+"F4.opPattern","COPY",BODY,{"derivedFrom":makeQuery(id+"F2.opPattern","COPY",BODY,{"derivedFrom":makeQuery(id+"F1.opRevolve","SWEPT_BODY",BODY,{"disambiguationData":[OSD([sQuery(id+"F0.wireOp",EDGE,"E1")])]}),"instanceName":"1"}),"instanceName":"1"}),"instanceName":"1"}),"instanceName":"1"}),"instanceName":"1"}),"instanceName":"1"});
            var Q929;
            Q929=makeQuery(id+"F12.opPattern","COPY",BODY,{"derivedFrom":makeQuery(id+"F9.opPattern","COPY",BODY,{"derivedFrom":makeQuery(id+"F8.opPattern","COPY",BODY,{"derivedFrom":makeQuery(id+"F6.opPattern","COPY",BODY,{"derivedFrom":makeQuery(id+"F4.opPattern","COPY",BODY,{"derivedFrom":makeQuery(id+"F3.opPattern","COPY",BODY,{"derivedFrom":makeQuery(id+"F2.opPattern","COPY",BODY,{"derivedFrom":makeQuery(id+"F1.opRevolve","SWEPT_BODY",BODY,{"disambiguationData":[OSD([sQuery(id+"F0.wireOp",EDGE,"E1")])]}),"instanceName":"1"}),"instanceName":"1"}),"instanceName":"1"}),"instanceName":"1"}),"instanceName":"1"}),"instanceName":"1"}),"instanceName":"1"});
            var Q930;
            Q930=makeQuery(id+"F12.opPattern","COPY",BODY,{"derivedFrom":makeQuery(id+"F9.opPattern","COPY",BODY,{"derivedFrom":makeQuery(id+"F8.opPattern","COPY",BODY,{"derivedFrom":makeQuery(id+"F6.opPattern","COPY",BODY,{"derivedFrom":makeQuery(id+"F5.opPattern","COPY",BODY,{"derivedFrom":makeQuery(id+"F1.opRevolve","SWEPT_BODY",BODY,{"disambiguationData":[OSD([sQuery(id+"F0.wireOp",EDGE,"E1")])]}),"instanceName":"1"}),"instanceName":"1"}),"instanceName":"1"}),"instanceName":"1"}),"instanceName":"1"});
            var Q931;
            Q931=makeQuery(id+"F12.opPattern","COPY",BODY,{"derivedFrom":makeQuery(id+"F9.opPattern","COPY",BODY,{"derivedFrom":makeQuery(id+"F8.opPattern","COPY",BODY,{"derivedFrom":makeQuery(id+"F6.opPattern","COPY",BODY,{"derivedFrom":makeQuery(id+"F5.opPattern","COPY",BODY,{"derivedFrom":makeQuery(id+"F2.opPattern","COPY",BODY,{"derivedFrom":makeQuery(id+"F1.opRevolve","SWEPT_BODY",BODY,{"disambiguationData":[OSD([sQuery(id+"F0.wireOp",EDGE,"E1")])]}),"instanceName":"1"}),"instanceName":"1"}),"instanceName":"1"}),"instanceName":"1"}),"instanceName":"1"}),"instanceName":"1"});
            var Q932;
            Q932=makeQuery(id+"F12.opPattern","COPY",BODY,{"derivedFrom":makeQuery(id+"F9.opPattern","COPY",BODY,{"derivedFrom":makeQuery(id+"F8.opPattern","COPY",BODY,{"derivedFrom":makeQuery(id+"F6.opPattern","COPY",BODY,{"derivedFrom":makeQuery(id+"F5.opPattern","COPY",BODY,{"derivedFrom":makeQuery(id+"F3.opPattern","COPY",BODY,{"derivedFrom":makeQuery(id+"F2.opPattern","COPY",BODY,{"derivedFrom":makeQuery(id+"F1.opRevolve","SWEPT_BODY",BODY,{"disambiguationData":[OSD([sQuery(id+"F0.wireOp",EDGE,"E1")])]}),"instanceName":"1"}),"instanceName":"1"}),"instanceName":"1"}),"instanceName":"1"}),"instanceName":"1"}),"instanceName":"1"}),"instanceName":"1"});
            var Q933;
            Q933=makeQuery(id+"F12.opPattern","COPY",BODY,{"derivedFrom":makeQuery(id+"F9.opPattern","COPY",BODY,{"derivedFrom":makeQuery(id+"F8.opPattern","COPY",BODY,{"derivedFrom":makeQuery(id+"F6.opPattern","COPY",BODY,{"derivedFrom":makeQuery(id+"F5.opPattern","COPY",BODY,{"derivedFrom":makeQuery(id+"F4.opPattern","COPY",BODY,{"derivedFrom":makeQuery(id+"F1.opRevolve","SWEPT_BODY",BODY,{"disambiguationData":[OSD([sQuery(id+"F0.wireOp",EDGE,"E1")])]}),"instanceName":"1"}),"instanceName":"1"}),"instanceName":"1"}),"instanceName":"1"}),"instanceName":"1"}),"instanceName":"1"});
            var Q934;
            Q934=makeQuery(id+"F12.opPattern","COPY",BODY,{"derivedFrom":makeQuery(id+"F9.opPattern","COPY",BODY,{"derivedFrom":makeQuery(id+"F8.opPattern","COPY",BODY,{"derivedFrom":makeQuery(id+"F6.opPattern","COPY",BODY,{"derivedFrom":makeQuery(id+"F5.opPattern","COPY",BODY,{"derivedFrom":makeQuery(id+"F4.opPattern","COPY",BODY,{"derivedFrom":makeQuery(id+"F2.opPattern","COPY",BODY,{"derivedFrom":makeQuery(id+"F1.opRevolve","SWEPT_BODY",BODY,{"disambiguationData":[OSD([sQuery(id+"F0.wireOp",EDGE,"E1")])]}),"instanceName":"1"}),"instanceName":"1"}),"instanceName":"1"}),"instanceName":"1"}),"instanceName":"1"}),"instanceName":"1"}),"instanceName":"1"});
            var Q935;
            Q935=makeQuery(id+"F12.opPattern","COPY",BODY,{"derivedFrom":makeQuery(id+"F9.opPattern","COPY",BODY,{"derivedFrom":makeQuery(id+"F8.opPattern","COPY",BODY,{"derivedFrom":makeQuery(id+"F6.opPattern","COPY",BODY,{"derivedFrom":makeQuery(id+"F5.opPattern","COPY",BODY,{"derivedFrom":makeQuery(id+"F4.opPattern","COPY",BODY,{"derivedFrom":makeQuery(id+"F3.opPattern","COPY",BODY,{"derivedFrom":makeQuery(id+"F2.opPattern","COPY",BODY,{"derivedFrom":makeQuery(id+"F1.opRevolve","SWEPT_BODY",BODY,{"disambiguationData":[OSD([sQuery(id+"F0.wireOp",EDGE,"E1")])]}),"instanceName":"1"}),"instanceName":"1"}),"instanceName":"1"}),"instanceName":"1"}),"instanceName":"1"}),"instanceName":"1"}),"instanceName":"1"}),"instanceName":"1"});
            var Q936;
            Q936=makeQuery(id+"F12.opPattern","COPY",BODY,{"derivedFrom":makeQuery(id+"F9.opPattern","COPY",BODY,{"derivedFrom":makeQuery(id+"F8.opPattern","COPY",BODY,{"derivedFrom":makeQuery(id+"F7.opPattern","COPY",BODY,{"derivedFrom":makeQuery(id+"F1.opRevolve","SWEPT_BODY",BODY,{"disambiguationData":[OSD([sQuery(id+"F0.wireOp",EDGE,"E1")])]}),"instanceName":"1"}),"instanceName":"1"}),"instanceName":"1"}),"instanceName":"1"});
            var Q937;
            Q937=makeQuery(id+"F12.opPattern","COPY",BODY,{"derivedFrom":makeQuery(id+"F9.opPattern","COPY",BODY,{"derivedFrom":makeQuery(id+"F8.opPattern","COPY",BODY,{"derivedFrom":makeQuery(id+"F7.opPattern","COPY",BODY,{"derivedFrom":makeQuery(id+"F2.opPattern","COPY",BODY,{"derivedFrom":makeQuery(id+"F1.opRevolve","SWEPT_BODY",BODY,{"disambiguationData":[OSD([sQuery(id+"F0.wireOp",EDGE,"E1")])]}),"instanceName":"1"}),"instanceName":"1"}),"instanceName":"1"}),"instanceName":"1"}),"instanceName":"1"});
            var Q938;
            Q938=makeQuery(id+"F12.opPattern","COPY",BODY,{"derivedFrom":makeQuery(id+"F9.opPattern","COPY",BODY,{"derivedFrom":makeQuery(id+"F8.opPattern","COPY",BODY,{"derivedFrom":makeQuery(id+"F7.opPattern","COPY",BODY,{"derivedFrom":makeQuery(id+"F3.opPattern","COPY",BODY,{"derivedFrom":makeQuery(id+"F2.opPattern","COPY",BODY,{"derivedFrom":makeQuery(id+"F1.opRevolve","SWEPT_BODY",BODY,{"disambiguationData":[OSD([sQuery(id+"F0.wireOp",EDGE,"E1")])]}),"instanceName":"1"}),"instanceName":"1"}),"instanceName":"1"}),"instanceName":"1"}),"instanceName":"1"}),"instanceName":"1"});
            var Q939;
            Q939=makeQuery(id+"F12.opPattern","COPY",BODY,{"derivedFrom":makeQuery(id+"F9.opPattern","COPY",BODY,{"derivedFrom":makeQuery(id+"F8.opPattern","COPY",BODY,{"derivedFrom":makeQuery(id+"F7.opPattern","COPY",BODY,{"derivedFrom":makeQuery(id+"F4.opPattern","COPY",BODY,{"derivedFrom":makeQuery(id+"F1.opRevolve","SWEPT_BODY",BODY,{"disambiguationData":[OSD([sQuery(id+"F0.wireOp",EDGE,"E1")])]}),"instanceName":"1"}),"instanceName":"1"}),"instanceName":"1"}),"instanceName":"1"}),"instanceName":"1"});
            var Q940;
            Q940=makeQuery(id+"F12.opPattern","COPY",BODY,{"derivedFrom":makeQuery(id+"F9.opPattern","COPY",BODY,{"derivedFrom":makeQuery(id+"F8.opPattern","COPY",BODY,{"derivedFrom":makeQuery(id+"F7.opPattern","COPY",BODY,{"derivedFrom":makeQuery(id+"F4.opPattern","COPY",BODY,{"derivedFrom":makeQuery(id+"F2.opPattern","COPY",BODY,{"derivedFrom":makeQuery(id+"F1.opRevolve","SWEPT_BODY",BODY,{"disambiguationData":[OSD([sQuery(id+"F0.wireOp",EDGE,"E1")])]}),"instanceName":"1"}),"instanceName":"1"}),"instanceName":"1"}),"instanceName":"1"}),"instanceName":"1"}),"instanceName":"1"});
            var Q941;
            Q941=makeQuery(id+"F12.opPattern","COPY",BODY,{"derivedFrom":makeQuery(id+"F9.opPattern","COPY",BODY,{"derivedFrom":makeQuery(id+"F8.opPattern","COPY",BODY,{"derivedFrom":makeQuery(id+"F7.opPattern","COPY",BODY,{"derivedFrom":makeQuery(id+"F4.opPattern","COPY",BODY,{"derivedFrom":makeQuery(id+"F3.opPattern","COPY",BODY,{"derivedFrom":makeQuery(id+"F2.opPattern","COPY",BODY,{"derivedFrom":makeQuery(id+"F1.opRevolve","SWEPT_BODY",BODY,{"disambiguationData":[OSD([sQuery(id+"F0.wireOp",EDGE,"E1")])]}),"instanceName":"1"}),"instanceName":"1"}),"instanceName":"1"}),"instanceName":"1"}),"instanceName":"1"}),"instanceName":"1"}),"instanceName":"1"});
            var Q942;
            Q942=makeQuery(id+"F12.opPattern","COPY",BODY,{"derivedFrom":makeQuery(id+"F9.opPattern","COPY",BODY,{"derivedFrom":makeQuery(id+"F8.opPattern","COPY",BODY,{"derivedFrom":makeQuery(id+"F7.opPattern","COPY",BODY,{"derivedFrom":makeQuery(id+"F5.opPattern","COPY",BODY,{"derivedFrom":makeQuery(id+"F1.opRevolve","SWEPT_BODY",BODY,{"disambiguationData":[OSD([sQuery(id+"F0.wireOp",EDGE,"E1")])]}),"instanceName":"1"}),"instanceName":"1"}),"instanceName":"1"}),"instanceName":"1"}),"instanceName":"1"});
            var Q943;
            Q943=makeQuery(id+"F12.opPattern","COPY",BODY,{"derivedFrom":makeQuery(id+"F9.opPattern","COPY",BODY,{"derivedFrom":makeQuery(id+"F8.opPattern","COPY",BODY,{"derivedFrom":makeQuery(id+"F7.opPattern","COPY",BODY,{"derivedFrom":makeQuery(id+"F5.opPattern","COPY",BODY,{"derivedFrom":makeQuery(id+"F2.opPattern","COPY",BODY,{"derivedFrom":makeQuery(id+"F1.opRevolve","SWEPT_BODY",BODY,{"disambiguationData":[OSD([sQuery(id+"F0.wireOp",EDGE,"E1")])]}),"instanceName":"1"}),"instanceName":"1"}),"instanceName":"1"}),"instanceName":"1"}),"instanceName":"1"}),"instanceName":"1"});
            var Q944;
            Q944=makeQuery(id+"F12.opPattern","COPY",BODY,{"derivedFrom":makeQuery(id+"F9.opPattern","COPY",BODY,{"derivedFrom":makeQuery(id+"F8.opPattern","COPY",BODY,{"derivedFrom":makeQuery(id+"F7.opPattern","COPY",BODY,{"derivedFrom":makeQuery(id+"F5.opPattern","COPY",BODY,{"derivedFrom":makeQuery(id+"F3.opPattern","COPY",BODY,{"derivedFrom":makeQuery(id+"F2.opPattern","COPY",BODY,{"derivedFrom":makeQuery(id+"F1.opRevolve","SWEPT_BODY",BODY,{"disambiguationData":[OSD([sQuery(id+"F0.wireOp",EDGE,"E1")])]}),"instanceName":"1"}),"instanceName":"1"}),"instanceName":"1"}),"instanceName":"1"}),"instanceName":"1"}),"instanceName":"1"}),"instanceName":"1"});
            var Q945;
            Q945=makeQuery(id+"F12.opPattern","COPY",BODY,{"derivedFrom":makeQuery(id+"F9.opPattern","COPY",BODY,{"derivedFrom":makeQuery(id+"F8.opPattern","COPY",BODY,{"derivedFrom":makeQuery(id+"F7.opPattern","COPY",BODY,{"derivedFrom":makeQuery(id+"F5.opPattern","COPY",BODY,{"derivedFrom":makeQuery(id+"F4.opPattern","COPY",BODY,{"derivedFrom":makeQuery(id+"F1.opRevolve","SWEPT_BODY",BODY,{"disambiguationData":[OSD([sQuery(id+"F0.wireOp",EDGE,"E1")])]}),"instanceName":"1"}),"instanceName":"1"}),"instanceName":"1"}),"instanceName":"1"}),"instanceName":"1"}),"instanceName":"1"});
            var Q946;
            Q946=makeQuery(id+"F12.opPattern","COPY",BODY,{"derivedFrom":makeQuery(id+"F9.opPattern","COPY",BODY,{"derivedFrom":makeQuery(id+"F8.opPattern","COPY",BODY,{"derivedFrom":makeQuery(id+"F7.opPattern","COPY",BODY,{"derivedFrom":makeQuery(id+"F5.opPattern","COPY",BODY,{"derivedFrom":makeQuery(id+"F4.opPattern","COPY",BODY,{"derivedFrom":makeQuery(id+"F2.opPattern","COPY",BODY,{"derivedFrom":makeQuery(id+"F1.opRevolve","SWEPT_BODY",BODY,{"disambiguationData":[OSD([sQuery(id+"F0.wireOp",EDGE,"E1")])]}),"instanceName":"1"}),"instanceName":"1"}),"instanceName":"1"}),"instanceName":"1"}),"instanceName":"1"}),"instanceName":"1"}),"instanceName":"1"});
            var Q947;
            Q947=makeQuery(id+"F12.opPattern","COPY",BODY,{"derivedFrom":makeQuery(id+"F9.opPattern","COPY",BODY,{"derivedFrom":makeQuery(id+"F8.opPattern","COPY",BODY,{"derivedFrom":makeQuery(id+"F7.opPattern","COPY",BODY,{"derivedFrom":makeQuery(id+"F5.opPattern","COPY",BODY,{"derivedFrom":makeQuery(id+"F4.opPattern","COPY",BODY,{"derivedFrom":makeQuery(id+"F3.opPattern","COPY",BODY,{"derivedFrom":makeQuery(id+"F2.opPattern","COPY",BODY,{"derivedFrom":makeQuery(id+"F1.opRevolve","SWEPT_BODY",BODY,{"disambiguationData":[OSD([sQuery(id+"F0.wireOp",EDGE,"E1")])]}),"instanceName":"1"}),"instanceName":"1"}),"instanceName":"1"}),"instanceName":"1"}),"instanceName":"1"}),"instanceName":"1"}),"instanceName":"1"}),"instanceName":"1"});
            var Q948;
            Q948=makeQuery(id+"F12.opPattern","COPY",BODY,{"derivedFrom":makeQuery(id+"F9.opPattern","COPY",BODY,{"derivedFrom":makeQuery(id+"F8.opPattern","COPY",BODY,{"derivedFrom":makeQuery(id+"F7.opPattern","COPY",BODY,{"derivedFrom":makeQuery(id+"F6.opPattern","COPY",BODY,{"derivedFrom":makeQuery(id+"F1.opRevolve","SWEPT_BODY",BODY,{"disambiguationData":[OSD([sQuery(id+"F0.wireOp",EDGE,"E1")])]}),"instanceName":"1"}),"instanceName":"1"}),"instanceName":"1"}),"instanceName":"1"}),"instanceName":"1"});
            var Q949;
            Q949=makeQuery(id+"F12.opPattern","COPY",BODY,{"derivedFrom":makeQuery(id+"F9.opPattern","COPY",BODY,{"derivedFrom":makeQuery(id+"F8.opPattern","COPY",BODY,{"derivedFrom":makeQuery(id+"F7.opPattern","COPY",BODY,{"derivedFrom":makeQuery(id+"F6.opPattern","COPY",BODY,{"derivedFrom":makeQuery(id+"F2.opPattern","COPY",BODY,{"derivedFrom":makeQuery(id+"F1.opRevolve","SWEPT_BODY",BODY,{"disambiguationData":[OSD([sQuery(id+"F0.wireOp",EDGE,"E1")])]}),"instanceName":"1"}),"instanceName":"1"}),"instanceName":"1"}),"instanceName":"1"}),"instanceName":"1"}),"instanceName":"1"});
            var Q950;
            Q950=makeQuery(id+"F12.opPattern","COPY",BODY,{"derivedFrom":makeQuery(id+"F9.opPattern","COPY",BODY,{"derivedFrom":makeQuery(id+"F8.opPattern","COPY",BODY,{"derivedFrom":makeQuery(id+"F7.opPattern","COPY",BODY,{"derivedFrom":makeQuery(id+"F6.opPattern","COPY",BODY,{"derivedFrom":makeQuery(id+"F3.opPattern","COPY",BODY,{"derivedFrom":makeQuery(id+"F2.opPattern","COPY",BODY,{"derivedFrom":makeQuery(id+"F1.opRevolve","SWEPT_BODY",BODY,{"disambiguationData":[OSD([sQuery(id+"F0.wireOp",EDGE,"E1")])]}),"instanceName":"1"}),"instanceName":"1"}),"instanceName":"1"}),"instanceName":"1"}),"instanceName":"1"}),"instanceName":"1"}),"instanceName":"1"});
            var Q951;
            Q951=makeQuery(id+"F12.opPattern","COPY",BODY,{"derivedFrom":makeQuery(id+"F9.opPattern","COPY",BODY,{"derivedFrom":makeQuery(id+"F8.opPattern","COPY",BODY,{"derivedFrom":makeQuery(id+"F7.opPattern","COPY",BODY,{"derivedFrom":makeQuery(id+"F6.opPattern","COPY",BODY,{"derivedFrom":makeQuery(id+"F4.opPattern","COPY",BODY,{"derivedFrom":makeQuery(id+"F1.opRevolve","SWEPT_BODY",BODY,{"disambiguationData":[OSD([sQuery(id+"F0.wireOp",EDGE,"E1")])]}),"instanceName":"1"}),"instanceName":"1"}),"instanceName":"1"}),"instanceName":"1"}),"instanceName":"1"}),"instanceName":"1"});
            var Q952;
            Q952=makeQuery(id+"F12.opPattern","COPY",BODY,{"derivedFrom":makeQuery(id+"F9.opPattern","COPY",BODY,{"derivedFrom":makeQuery(id+"F8.opPattern","COPY",BODY,{"derivedFrom":makeQuery(id+"F7.opPattern","COPY",BODY,{"derivedFrom":makeQuery(id+"F6.opPattern","COPY",BODY,{"derivedFrom":makeQuery(id+"F4.opPattern","COPY",BODY,{"derivedFrom":makeQuery(id+"F2.opPattern","COPY",BODY,{"derivedFrom":makeQuery(id+"F1.opRevolve","SWEPT_BODY",BODY,{"disambiguationData":[OSD([sQuery(id+"F0.wireOp",EDGE,"E1")])]}),"instanceName":"1"}),"instanceName":"1"}),"instanceName":"1"}),"instanceName":"1"}),"instanceName":"1"}),"instanceName":"1"}),"instanceName":"1"});
            var Q953;
            Q953=makeQuery(id+"F12.opPattern","COPY",BODY,{"derivedFrom":makeQuery(id+"F9.opPattern","COPY",BODY,{"derivedFrom":makeQuery(id+"F8.opPattern","COPY",BODY,{"derivedFrom":makeQuery(id+"F7.opPattern","COPY",BODY,{"derivedFrom":makeQuery(id+"F6.opPattern","COPY",BODY,{"derivedFrom":makeQuery(id+"F4.opPattern","COPY",BODY,{"derivedFrom":makeQuery(id+"F3.opPattern","COPY",BODY,{"derivedFrom":makeQuery(id+"F2.opPattern","COPY",BODY,{"derivedFrom":makeQuery(id+"F1.opRevolve","SWEPT_BODY",BODY,{"disambiguationData":[OSD([sQuery(id+"F0.wireOp",EDGE,"E1")])]}),"instanceName":"1"}),"instanceName":"1"}),"instanceName":"1"}),"instanceName":"1"}),"instanceName":"1"}),"instanceName":"1"}),"instanceName":"1"}),"instanceName":"1"});
            var Q954;
            Q954=makeQuery(id+"F12.opPattern","COPY",BODY,{"derivedFrom":makeQuery(id+"F9.opPattern","COPY",BODY,{"derivedFrom":makeQuery(id+"F8.opPattern","COPY",BODY,{"derivedFrom":makeQuery(id+"F7.opPattern","COPY",BODY,{"derivedFrom":makeQuery(id+"F6.opPattern","COPY",BODY,{"derivedFrom":makeQuery(id+"F5.opPattern","COPY",BODY,{"derivedFrom":makeQuery(id+"F1.opRevolve","SWEPT_BODY",BODY,{"disambiguationData":[OSD([sQuery(id+"F0.wireOp",EDGE,"E1")])]}),"instanceName":"1"}),"instanceName":"1"}),"instanceName":"1"}),"instanceName":"1"}),"instanceName":"1"}),"instanceName":"1"});
            var Q955;
            Q955=makeQuery(id+"F12.opPattern","COPY",BODY,{"derivedFrom":makeQuery(id+"F9.opPattern","COPY",BODY,{"derivedFrom":makeQuery(id+"F8.opPattern","COPY",BODY,{"derivedFrom":makeQuery(id+"F7.opPattern","COPY",BODY,{"derivedFrom":makeQuery(id+"F6.opPattern","COPY",BODY,{"derivedFrom":makeQuery(id+"F5.opPattern","COPY",BODY,{"derivedFrom":makeQuery(id+"F2.opPattern","COPY",BODY,{"derivedFrom":makeQuery(id+"F1.opRevolve","SWEPT_BODY",BODY,{"disambiguationData":[OSD([sQuery(id+"F0.wireOp",EDGE,"E1")])]}),"instanceName":"1"}),"instanceName":"1"}),"instanceName":"1"}),"instanceName":"1"}),"instanceName":"1"}),"instanceName":"1"}),"instanceName":"1"});
            var Q956;
            Q956=makeQuery(id+"F12.opPattern","COPY",BODY,{"derivedFrom":makeQuery(id+"F9.opPattern","COPY",BODY,{"derivedFrom":makeQuery(id+"F8.opPattern","COPY",BODY,{"derivedFrom":makeQuery(id+"F7.opPattern","COPY",BODY,{"derivedFrom":makeQuery(id+"F6.opPattern","COPY",BODY,{"derivedFrom":makeQuery(id+"F5.opPattern","COPY",BODY,{"derivedFrom":makeQuery(id+"F3.opPattern","COPY",BODY,{"derivedFrom":makeQuery(id+"F2.opPattern","COPY",BODY,{"derivedFrom":makeQuery(id+"F1.opRevolve","SWEPT_BODY",BODY,{"disambiguationData":[OSD([sQuery(id+"F0.wireOp",EDGE,"E1")])]}),"instanceName":"1"}),"instanceName":"1"}),"instanceName":"1"}),"instanceName":"1"}),"instanceName":"1"}),"instanceName":"1"}),"instanceName":"1"}),"instanceName":"1"});
            var Q957;
            Q957=makeQuery(id+"F12.opPattern","COPY",BODY,{"derivedFrom":makeQuery(id+"F9.opPattern","COPY",BODY,{"derivedFrom":makeQuery(id+"F8.opPattern","COPY",BODY,{"derivedFrom":makeQuery(id+"F7.opPattern","COPY",BODY,{"derivedFrom":makeQuery(id+"F6.opPattern","COPY",BODY,{"derivedFrom":makeQuery(id+"F5.opPattern","COPY",BODY,{"derivedFrom":makeQuery(id+"F4.opPattern","COPY",BODY,{"derivedFrom":makeQuery(id+"F1.opRevolve","SWEPT_BODY",BODY,{"disambiguationData":[OSD([sQuery(id+"F0.wireOp",EDGE,"E1")])]}),"instanceName":"1"}),"instanceName":"1"}),"instanceName":"1"}),"instanceName":"1"}),"instanceName":"1"}),"instanceName":"1"}),"instanceName":"1"});
            var Q958;
            Q958=makeQuery(id+"F12.opPattern","COPY",BODY,{"derivedFrom":makeQuery(id+"F9.opPattern","COPY",BODY,{"derivedFrom":makeQuery(id+"F8.opPattern","COPY",BODY,{"derivedFrom":makeQuery(id+"F7.opPattern","COPY",BODY,{"derivedFrom":makeQuery(id+"F6.opPattern","COPY",BODY,{"derivedFrom":makeQuery(id+"F5.opPattern","COPY",BODY,{"derivedFrom":makeQuery(id+"F4.opPattern","COPY",BODY,{"derivedFrom":makeQuery(id+"F2.opPattern","COPY",BODY,{"derivedFrom":makeQuery(id+"F1.opRevolve","SWEPT_BODY",BODY,{"disambiguationData":[OSD([sQuery(id+"F0.wireOp",EDGE,"E1")])]}),"instanceName":"1"}),"instanceName":"1"}),"instanceName":"1"}),"instanceName":"1"}),"instanceName":"1"}),"instanceName":"1"}),"instanceName":"1"}),"instanceName":"1"});
            var Q959;
            Q959=makeQuery(id+"F12.opPattern","COPY",BODY,{"derivedFrom":makeQuery(id+"F9.opPattern","COPY",BODY,{"derivedFrom":makeQuery(id+"F8.opPattern","COPY",BODY,{"derivedFrom":makeQuery(id+"F7.opPattern","COPY",BODY,{"derivedFrom":makeQuery(id+"F6.opPattern","COPY",BODY,{"derivedFrom":makeQuery(id+"F5.opPattern","COPY",BODY,{"derivedFrom":makeQuery(id+"F4.opPattern","COPY",BODY,{"derivedFrom":makeQuery(id+"F3.opPattern","COPY",BODY,{"derivedFrom":makeQuery(id+"F2.opPattern","COPY",BODY,{"derivedFrom":makeQuery(id+"F1.opRevolve","SWEPT_BODY",BODY,{"disambiguationData":[OSD([sQuery(id+"F0.wireOp",EDGE,"E1")])]}),"instanceName":"1"}),"instanceName":"1"}),"instanceName":"1"}),"instanceName":"1"}),"instanceName":"1"}),"instanceName":"1"}),"instanceName":"1"}),"instanceName":"1"}),"instanceName":"1"});
            var Q960;
            Q960=makeQuery(id+"F12.opPattern","COPY",BODY,{"derivedFrom":makeQuery(id+"F10.opPattern","COPY",BODY,{"derivedFrom":makeQuery(id+"F1.opRevolve","SWEPT_BODY",BODY,{"disambiguationData":[OSD([sQuery(id+"F0.wireOp",EDGE,"E1")])]}),"instanceName":"1"}),"instanceName":"1"});
            var Q961;
            Q961=makeQuery(id+"F12.opPattern","COPY",BODY,{"derivedFrom":makeQuery(id+"F10.opPattern","COPY",BODY,{"derivedFrom":makeQuery(id+"F2.opPattern","COPY",BODY,{"derivedFrom":makeQuery(id+"F1.opRevolve","SWEPT_BODY",BODY,{"disambiguationData":[OSD([sQuery(id+"F0.wireOp",EDGE,"E1")])]}),"instanceName":"1"}),"instanceName":"1"}),"instanceName":"1"});
            var Q962;
            Q962=makeQuery(id+"F12.opPattern","COPY",BODY,{"derivedFrom":makeQuery(id+"F10.opPattern","COPY",BODY,{"derivedFrom":makeQuery(id+"F3.opPattern","COPY",BODY,{"derivedFrom":makeQuery(id+"F2.opPattern","COPY",BODY,{"derivedFrom":makeQuery(id+"F1.opRevolve","SWEPT_BODY",BODY,{"disambiguationData":[OSD([sQuery(id+"F0.wireOp",EDGE,"E1")])]}),"instanceName":"1"}),"instanceName":"1"}),"instanceName":"1"}),"instanceName":"1"});
            var Q963;
            Q963=makeQuery(id+"F12.opPattern","COPY",BODY,{"derivedFrom":makeQuery(id+"F10.opPattern","COPY",BODY,{"derivedFrom":makeQuery(id+"F4.opPattern","COPY",BODY,{"derivedFrom":makeQuery(id+"F1.opRevolve","SWEPT_BODY",BODY,{"disambiguationData":[OSD([sQuery(id+"F0.wireOp",EDGE,"E1")])]}),"instanceName":"1"}),"instanceName":"1"}),"instanceName":"1"});
            var Q964;
            Q964=makeQuery(id+"F12.opPattern","COPY",BODY,{"derivedFrom":makeQuery(id+"F10.opPattern","COPY",BODY,{"derivedFrom":makeQuery(id+"F4.opPattern","COPY",BODY,{"derivedFrom":makeQuery(id+"F2.opPattern","COPY",BODY,{"derivedFrom":makeQuery(id+"F1.opRevolve","SWEPT_BODY",BODY,{"disambiguationData":[OSD([sQuery(id+"F0.wireOp",EDGE,"E1")])]}),"instanceName":"1"}),"instanceName":"1"}),"instanceName":"1"}),"instanceName":"1"});
            var Q965;
            Q965=makeQuery(id+"F12.opPattern","COPY",BODY,{"derivedFrom":makeQuery(id+"F10.opPattern","COPY",BODY,{"derivedFrom":makeQuery(id+"F4.opPattern","COPY",BODY,{"derivedFrom":makeQuery(id+"F3.opPattern","COPY",BODY,{"derivedFrom":makeQuery(id+"F2.opPattern","COPY",BODY,{"derivedFrom":makeQuery(id+"F1.opRevolve","SWEPT_BODY",BODY,{"disambiguationData":[OSD([sQuery(id+"F0.wireOp",EDGE,"E1")])]}),"instanceName":"1"}),"instanceName":"1"}),"instanceName":"1"}),"instanceName":"1"}),"instanceName":"1"});
            var Q966;
            Q966=makeQuery(id+"F12.opPattern","COPY",BODY,{"derivedFrom":makeQuery(id+"F10.opPattern","COPY",BODY,{"derivedFrom":makeQuery(id+"F5.opPattern","COPY",BODY,{"derivedFrom":makeQuery(id+"F1.opRevolve","SWEPT_BODY",BODY,{"disambiguationData":[OSD([sQuery(id+"F0.wireOp",EDGE,"E1")])]}),"instanceName":"1"}),"instanceName":"1"}),"instanceName":"1"});
            var Q967;
            Q967=makeQuery(id+"F12.opPattern","COPY",BODY,{"derivedFrom":makeQuery(id+"F10.opPattern","COPY",BODY,{"derivedFrom":makeQuery(id+"F5.opPattern","COPY",BODY,{"derivedFrom":makeQuery(id+"F2.opPattern","COPY",BODY,{"derivedFrom":makeQuery(id+"F1.opRevolve","SWEPT_BODY",BODY,{"disambiguationData":[OSD([sQuery(id+"F0.wireOp",EDGE,"E1")])]}),"instanceName":"1"}),"instanceName":"1"}),"instanceName":"1"}),"instanceName":"1"});
            var Q968;
            Q968=makeQuery(id+"F12.opPattern","COPY",BODY,{"derivedFrom":makeQuery(id+"F10.opPattern","COPY",BODY,{"derivedFrom":makeQuery(id+"F5.opPattern","COPY",BODY,{"derivedFrom":makeQuery(id+"F3.opPattern","COPY",BODY,{"derivedFrom":makeQuery(id+"F2.opPattern","COPY",BODY,{"derivedFrom":makeQuery(id+"F1.opRevolve","SWEPT_BODY",BODY,{"disambiguationData":[OSD([sQuery(id+"F0.wireOp",EDGE,"E1")])]}),"instanceName":"1"}),"instanceName":"1"}),"instanceName":"1"}),"instanceName":"1"}),"instanceName":"1"});
            var Q969;
            Q969=makeQuery(id+"F12.opPattern","COPY",BODY,{"derivedFrom":makeQuery(id+"F10.opPattern","COPY",BODY,{"derivedFrom":makeQuery(id+"F5.opPattern","COPY",BODY,{"derivedFrom":makeQuery(id+"F4.opPattern","COPY",BODY,{"derivedFrom":makeQuery(id+"F1.opRevolve","SWEPT_BODY",BODY,{"disambiguationData":[OSD([sQuery(id+"F0.wireOp",EDGE,"E1")])]}),"instanceName":"1"}),"instanceName":"1"}),"instanceName":"1"}),"instanceName":"1"});
            var Q970;
            Q970=makeQuery(id+"F12.opPattern","COPY",BODY,{"derivedFrom":makeQuery(id+"F10.opPattern","COPY",BODY,{"derivedFrom":makeQuery(id+"F5.opPattern","COPY",BODY,{"derivedFrom":makeQuery(id+"F4.opPattern","COPY",BODY,{"derivedFrom":makeQuery(id+"F2.opPattern","COPY",BODY,{"derivedFrom":makeQuery(id+"F1.opRevolve","SWEPT_BODY",BODY,{"disambiguationData":[OSD([sQuery(id+"F0.wireOp",EDGE,"E1")])]}),"instanceName":"1"}),"instanceName":"1"}),"instanceName":"1"}),"instanceName":"1"}),"instanceName":"1"});
            var Q971;
            Q971=makeQuery(id+"F12.opPattern","COPY",BODY,{"derivedFrom":makeQuery(id+"F10.opPattern","COPY",BODY,{"derivedFrom":makeQuery(id+"F5.opPattern","COPY",BODY,{"derivedFrom":makeQuery(id+"F4.opPattern","COPY",BODY,{"derivedFrom":makeQuery(id+"F3.opPattern","COPY",BODY,{"derivedFrom":makeQuery(id+"F2.opPattern","COPY",BODY,{"derivedFrom":makeQuery(id+"F1.opRevolve","SWEPT_BODY",BODY,{"disambiguationData":[OSD([sQuery(id+"F0.wireOp",EDGE,"E1")])]}),"instanceName":"1"}),"instanceName":"1"}),"instanceName":"1"}),"instanceName":"1"}),"instanceName":"1"}),"instanceName":"1"});
            var Q972;
            Q972=makeQuery(id+"F12.opPattern","COPY",BODY,{"derivedFrom":makeQuery(id+"F10.opPattern","COPY",BODY,{"derivedFrom":makeQuery(id+"F6.opPattern","COPY",BODY,{"derivedFrom":makeQuery(id+"F1.opRevolve","SWEPT_BODY",BODY,{"disambiguationData":[OSD([sQuery(id+"F0.wireOp",EDGE,"E1")])]}),"instanceName":"1"}),"instanceName":"1"}),"instanceName":"1"});
            var Q973;
            Q973=makeQuery(id+"F12.opPattern","COPY",BODY,{"derivedFrom":makeQuery(id+"F10.opPattern","COPY",BODY,{"derivedFrom":makeQuery(id+"F6.opPattern","COPY",BODY,{"derivedFrom":makeQuery(id+"F2.opPattern","COPY",BODY,{"derivedFrom":makeQuery(id+"F1.opRevolve","SWEPT_BODY",BODY,{"disambiguationData":[OSD([sQuery(id+"F0.wireOp",EDGE,"E1")])]}),"instanceName":"1"}),"instanceName":"1"}),"instanceName":"1"}),"instanceName":"1"});
            var Q974;
            Q974=makeQuery(id+"F12.opPattern","COPY",BODY,{"derivedFrom":makeQuery(id+"F10.opPattern","COPY",BODY,{"derivedFrom":makeQuery(id+"F6.opPattern","COPY",BODY,{"derivedFrom":makeQuery(id+"F3.opPattern","COPY",BODY,{"derivedFrom":makeQuery(id+"F2.opPattern","COPY",BODY,{"derivedFrom":makeQuery(id+"F1.opRevolve","SWEPT_BODY",BODY,{"disambiguationData":[OSD([sQuery(id+"F0.wireOp",EDGE,"E1")])]}),"instanceName":"1"}),"instanceName":"1"}),"instanceName":"1"}),"instanceName":"1"}),"instanceName":"1"});
            var Q975;
            Q975=makeQuery(id+"F12.opPattern","COPY",BODY,{"derivedFrom":makeQuery(id+"F10.opPattern","COPY",BODY,{"derivedFrom":makeQuery(id+"F6.opPattern","COPY",BODY,{"derivedFrom":makeQuery(id+"F4.opPattern","COPY",BODY,{"derivedFrom":makeQuery(id+"F1.opRevolve","SWEPT_BODY",BODY,{"disambiguationData":[OSD([sQuery(id+"F0.wireOp",EDGE,"E1")])]}),"instanceName":"1"}),"instanceName":"1"}),"instanceName":"1"}),"instanceName":"1"});
            var Q976;
            Q976=makeQuery(id+"F12.opPattern","COPY",BODY,{"derivedFrom":makeQuery(id+"F10.opPattern","COPY",BODY,{"derivedFrom":makeQuery(id+"F6.opPattern","COPY",BODY,{"derivedFrom":makeQuery(id+"F4.opPattern","COPY",BODY,{"derivedFrom":makeQuery(id+"F2.opPattern","COPY",BODY,{"derivedFrom":makeQuery(id+"F1.opRevolve","SWEPT_BODY",BODY,{"disambiguationData":[OSD([sQuery(id+"F0.wireOp",EDGE,"E1")])]}),"instanceName":"1"}),"instanceName":"1"}),"instanceName":"1"}),"instanceName":"1"}),"instanceName":"1"});
            var Q977;
            Q977=makeQuery(id+"F12.opPattern","COPY",BODY,{"derivedFrom":makeQuery(id+"F10.opPattern","COPY",BODY,{"derivedFrom":makeQuery(id+"F6.opPattern","COPY",BODY,{"derivedFrom":makeQuery(id+"F4.opPattern","COPY",BODY,{"derivedFrom":makeQuery(id+"F3.opPattern","COPY",BODY,{"derivedFrom":makeQuery(id+"F2.opPattern","COPY",BODY,{"derivedFrom":makeQuery(id+"F1.opRevolve","SWEPT_BODY",BODY,{"disambiguationData":[OSD([sQuery(id+"F0.wireOp",EDGE,"E1")])]}),"instanceName":"1"}),"instanceName":"1"}),"instanceName":"1"}),"instanceName":"1"}),"instanceName":"1"}),"instanceName":"1"});
            var Q978;
            Q978=makeQuery(id+"F12.opPattern","COPY",BODY,{"derivedFrom":makeQuery(id+"F10.opPattern","COPY",BODY,{"derivedFrom":makeQuery(id+"F6.opPattern","COPY",BODY,{"derivedFrom":makeQuery(id+"F5.opPattern","COPY",BODY,{"derivedFrom":makeQuery(id+"F1.opRevolve","SWEPT_BODY",BODY,{"disambiguationData":[OSD([sQuery(id+"F0.wireOp",EDGE,"E1")])]}),"instanceName":"1"}),"instanceName":"1"}),"instanceName":"1"}),"instanceName":"1"});
            var Q979;
            Q979=makeQuery(id+"F12.opPattern","COPY",BODY,{"derivedFrom":makeQuery(id+"F10.opPattern","COPY",BODY,{"derivedFrom":makeQuery(id+"F6.opPattern","COPY",BODY,{"derivedFrom":makeQuery(id+"F5.opPattern","COPY",BODY,{"derivedFrom":makeQuery(id+"F2.opPattern","COPY",BODY,{"derivedFrom":makeQuery(id+"F1.opRevolve","SWEPT_BODY",BODY,{"disambiguationData":[OSD([sQuery(id+"F0.wireOp",EDGE,"E1")])]}),"instanceName":"1"}),"instanceName":"1"}),"instanceName":"1"}),"instanceName":"1"}),"instanceName":"1"});
            var Q980;
            Q980=makeQuery(id+"F12.opPattern","COPY",BODY,{"derivedFrom":makeQuery(id+"F10.opPattern","COPY",BODY,{"derivedFrom":makeQuery(id+"F6.opPattern","COPY",BODY,{"derivedFrom":makeQuery(id+"F5.opPattern","COPY",BODY,{"derivedFrom":makeQuery(id+"F3.opPattern","COPY",BODY,{"derivedFrom":makeQuery(id+"F2.opPattern","COPY",BODY,{"derivedFrom":makeQuery(id+"F1.opRevolve","SWEPT_BODY",BODY,{"disambiguationData":[OSD([sQuery(id+"F0.wireOp",EDGE,"E1")])]}),"instanceName":"1"}),"instanceName":"1"}),"instanceName":"1"}),"instanceName":"1"}),"instanceName":"1"}),"instanceName":"1"});
            var Q981;
            Q981=makeQuery(id+"F12.opPattern","COPY",BODY,{"derivedFrom":makeQuery(id+"F10.opPattern","COPY",BODY,{"derivedFrom":makeQuery(id+"F6.opPattern","COPY",BODY,{"derivedFrom":makeQuery(id+"F5.opPattern","COPY",BODY,{"derivedFrom":makeQuery(id+"F4.opPattern","COPY",BODY,{"derivedFrom":makeQuery(id+"F1.opRevolve","SWEPT_BODY",BODY,{"disambiguationData":[OSD([sQuery(id+"F0.wireOp",EDGE,"E1")])]}),"instanceName":"1"}),"instanceName":"1"}),"instanceName":"1"}),"instanceName":"1"}),"instanceName":"1"});
            var Q982;
            Q982=makeQuery(id+"F12.opPattern","COPY",BODY,{"derivedFrom":makeQuery(id+"F10.opPattern","COPY",BODY,{"derivedFrom":makeQuery(id+"F6.opPattern","COPY",BODY,{"derivedFrom":makeQuery(id+"F5.opPattern","COPY",BODY,{"derivedFrom":makeQuery(id+"F4.opPattern","COPY",BODY,{"derivedFrom":makeQuery(id+"F2.opPattern","COPY",BODY,{"derivedFrom":makeQuery(id+"F1.opRevolve","SWEPT_BODY",BODY,{"disambiguationData":[OSD([sQuery(id+"F0.wireOp",EDGE,"E1")])]}),"instanceName":"1"}),"instanceName":"1"}),"instanceName":"1"}),"instanceName":"1"}),"instanceName":"1"}),"instanceName":"1"});
            var Q983;
            Q983=makeQuery(id+"F12.opPattern","COPY",BODY,{"derivedFrom":makeQuery(id+"F10.opPattern","COPY",BODY,{"derivedFrom":makeQuery(id+"F6.opPattern","COPY",BODY,{"derivedFrom":makeQuery(id+"F5.opPattern","COPY",BODY,{"derivedFrom":makeQuery(id+"F4.opPattern","COPY",BODY,{"derivedFrom":makeQuery(id+"F3.opPattern","COPY",BODY,{"derivedFrom":makeQuery(id+"F2.opPattern","COPY",BODY,{"derivedFrom":makeQuery(id+"F1.opRevolve","SWEPT_BODY",BODY,{"disambiguationData":[OSD([sQuery(id+"F0.wireOp",EDGE,"E1")])]}),"instanceName":"1"}),"instanceName":"1"}),"instanceName":"1"}),"instanceName":"1"}),"instanceName":"1"}),"instanceName":"1"}),"instanceName":"1"});
            var Q984;
            Q984=makeQuery(id+"F12.opPattern","COPY",BODY,{"derivedFrom":makeQuery(id+"F10.opPattern","COPY",BODY,{"derivedFrom":makeQuery(id+"F7.opPattern","COPY",BODY,{"derivedFrom":makeQuery(id+"F1.opRevolve","SWEPT_BODY",BODY,{"disambiguationData":[OSD([sQuery(id+"F0.wireOp",EDGE,"E1")])]}),"instanceName":"1"}),"instanceName":"1"}),"instanceName":"1"});
            var Q985;
            Q985=makeQuery(id+"F12.opPattern","COPY",BODY,{"derivedFrom":makeQuery(id+"F10.opPattern","COPY",BODY,{"derivedFrom":makeQuery(id+"F7.opPattern","COPY",BODY,{"derivedFrom":makeQuery(id+"F2.opPattern","COPY",BODY,{"derivedFrom":makeQuery(id+"F1.opRevolve","SWEPT_BODY",BODY,{"disambiguationData":[OSD([sQuery(id+"F0.wireOp",EDGE,"E1")])]}),"instanceName":"1"}),"instanceName":"1"}),"instanceName":"1"}),"instanceName":"1"});
            var Q986;
            Q986=makeQuery(id+"F12.opPattern","COPY",BODY,{"derivedFrom":makeQuery(id+"F10.opPattern","COPY",BODY,{"derivedFrom":makeQuery(id+"F7.opPattern","COPY",BODY,{"derivedFrom":makeQuery(id+"F3.opPattern","COPY",BODY,{"derivedFrom":makeQuery(id+"F2.opPattern","COPY",BODY,{"derivedFrom":makeQuery(id+"F1.opRevolve","SWEPT_BODY",BODY,{"disambiguationData":[OSD([sQuery(id+"F0.wireOp",EDGE,"E1")])]}),"instanceName":"1"}),"instanceName":"1"}),"instanceName":"1"}),"instanceName":"1"}),"instanceName":"1"});
            var Q987;
            Q987=makeQuery(id+"F12.opPattern","COPY",BODY,{"derivedFrom":makeQuery(id+"F10.opPattern","COPY",BODY,{"derivedFrom":makeQuery(id+"F7.opPattern","COPY",BODY,{"derivedFrom":makeQuery(id+"F4.opPattern","COPY",BODY,{"derivedFrom":makeQuery(id+"F1.opRevolve","SWEPT_BODY",BODY,{"disambiguationData":[OSD([sQuery(id+"F0.wireOp",EDGE,"E1")])]}),"instanceName":"1"}),"instanceName":"1"}),"instanceName":"1"}),"instanceName":"1"});
            var Q988;
            Q988=makeQuery(id+"F12.opPattern","COPY",BODY,{"derivedFrom":makeQuery(id+"F10.opPattern","COPY",BODY,{"derivedFrom":makeQuery(id+"F7.opPattern","COPY",BODY,{"derivedFrom":makeQuery(id+"F4.opPattern","COPY",BODY,{"derivedFrom":makeQuery(id+"F2.opPattern","COPY",BODY,{"derivedFrom":makeQuery(id+"F1.opRevolve","SWEPT_BODY",BODY,{"disambiguationData":[OSD([sQuery(id+"F0.wireOp",EDGE,"E1")])]}),"instanceName":"1"}),"instanceName":"1"}),"instanceName":"1"}),"instanceName":"1"}),"instanceName":"1"});
            var Q989;
            Q989=makeQuery(id+"F12.opPattern","COPY",BODY,{"derivedFrom":makeQuery(id+"F10.opPattern","COPY",BODY,{"derivedFrom":makeQuery(id+"F7.opPattern","COPY",BODY,{"derivedFrom":makeQuery(id+"F4.opPattern","COPY",BODY,{"derivedFrom":makeQuery(id+"F3.opPattern","COPY",BODY,{"derivedFrom":makeQuery(id+"F2.opPattern","COPY",BODY,{"derivedFrom":makeQuery(id+"F1.opRevolve","SWEPT_BODY",BODY,{"disambiguationData":[OSD([sQuery(id+"F0.wireOp",EDGE,"E1")])]}),"instanceName":"1"}),"instanceName":"1"}),"instanceName":"1"}),"instanceName":"1"}),"instanceName":"1"}),"instanceName":"1"});
            var Q990;
            Q990=makeQuery(id+"F12.opPattern","COPY",BODY,{"derivedFrom":makeQuery(id+"F10.opPattern","COPY",BODY,{"derivedFrom":makeQuery(id+"F7.opPattern","COPY",BODY,{"derivedFrom":makeQuery(id+"F5.opPattern","COPY",BODY,{"derivedFrom":makeQuery(id+"F1.opRevolve","SWEPT_BODY",BODY,{"disambiguationData":[OSD([sQuery(id+"F0.wireOp",EDGE,"E1")])]}),"instanceName":"1"}),"instanceName":"1"}),"instanceName":"1"}),"instanceName":"1"});
            var Q991;
            Q991=makeQuery(id+"F12.opPattern","COPY",BODY,{"derivedFrom":makeQuery(id+"F10.opPattern","COPY",BODY,{"derivedFrom":makeQuery(id+"F7.opPattern","COPY",BODY,{"derivedFrom":makeQuery(id+"F5.opPattern","COPY",BODY,{"derivedFrom":makeQuery(id+"F2.opPattern","COPY",BODY,{"derivedFrom":makeQuery(id+"F1.opRevolve","SWEPT_BODY",BODY,{"disambiguationData":[OSD([sQuery(id+"F0.wireOp",EDGE,"E1")])]}),"instanceName":"1"}),"instanceName":"1"}),"instanceName":"1"}),"instanceName":"1"}),"instanceName":"1"});
            var Q992;
            Q992=makeQuery(id+"F12.opPattern","COPY",BODY,{"derivedFrom":makeQuery(id+"F10.opPattern","COPY",BODY,{"derivedFrom":makeQuery(id+"F7.opPattern","COPY",BODY,{"derivedFrom":makeQuery(id+"F5.opPattern","COPY",BODY,{"derivedFrom":makeQuery(id+"F3.opPattern","COPY",BODY,{"derivedFrom":makeQuery(id+"F2.opPattern","COPY",BODY,{"derivedFrom":makeQuery(id+"F1.opRevolve","SWEPT_BODY",BODY,{"disambiguationData":[OSD([sQuery(id+"F0.wireOp",EDGE,"E1")])]}),"instanceName":"1"}),"instanceName":"1"}),"instanceName":"1"}),"instanceName":"1"}),"instanceName":"1"}),"instanceName":"1"});
            var Q993;
            Q993=makeQuery(id+"F12.opPattern","COPY",BODY,{"derivedFrom":makeQuery(id+"F10.opPattern","COPY",BODY,{"derivedFrom":makeQuery(id+"F7.opPattern","COPY",BODY,{"derivedFrom":makeQuery(id+"F5.opPattern","COPY",BODY,{"derivedFrom":makeQuery(id+"F4.opPattern","COPY",BODY,{"derivedFrom":makeQuery(id+"F1.opRevolve","SWEPT_BODY",BODY,{"disambiguationData":[OSD([sQuery(id+"F0.wireOp",EDGE,"E1")])]}),"instanceName":"1"}),"instanceName":"1"}),"instanceName":"1"}),"instanceName":"1"}),"instanceName":"1"});
            var Q994;
            Q994=makeQuery(id+"F12.opPattern","COPY",BODY,{"derivedFrom":makeQuery(id+"F10.opPattern","COPY",BODY,{"derivedFrom":makeQuery(id+"F7.opPattern","COPY",BODY,{"derivedFrom":makeQuery(id+"F5.opPattern","COPY",BODY,{"derivedFrom":makeQuery(id+"F4.opPattern","COPY",BODY,{"derivedFrom":makeQuery(id+"F2.opPattern","COPY",BODY,{"derivedFrom":makeQuery(id+"F1.opRevolve","SWEPT_BODY",BODY,{"disambiguationData":[OSD([sQuery(id+"F0.wireOp",EDGE,"E1")])]}),"instanceName":"1"}),"instanceName":"1"}),"instanceName":"1"}),"instanceName":"1"}),"instanceName":"1"}),"instanceName":"1"});
            var Q995;
            Q995=makeQuery(id+"F12.opPattern","COPY",BODY,{"derivedFrom":makeQuery(id+"F10.opPattern","COPY",BODY,{"derivedFrom":makeQuery(id+"F7.opPattern","COPY",BODY,{"derivedFrom":makeQuery(id+"F5.opPattern","COPY",BODY,{"derivedFrom":makeQuery(id+"F4.opPattern","COPY",BODY,{"derivedFrom":makeQuery(id+"F3.opPattern","COPY",BODY,{"derivedFrom":makeQuery(id+"F2.opPattern","COPY",BODY,{"derivedFrom":makeQuery(id+"F1.opRevolve","SWEPT_BODY",BODY,{"disambiguationData":[OSD([sQuery(id+"F0.wireOp",EDGE,"E1")])]}),"instanceName":"1"}),"instanceName":"1"}),"instanceName":"1"}),"instanceName":"1"}),"instanceName":"1"}),"instanceName":"1"}),"instanceName":"1"});
            var Q996;
            Q996=makeQuery(id+"F12.opPattern","COPY",BODY,{"derivedFrom":makeQuery(id+"F10.opPattern","COPY",BODY,{"derivedFrom":makeQuery(id+"F7.opPattern","COPY",BODY,{"derivedFrom":makeQuery(id+"F6.opPattern","COPY",BODY,{"derivedFrom":makeQuery(id+"F1.opRevolve","SWEPT_BODY",BODY,{"disambiguationData":[OSD([sQuery(id+"F0.wireOp",EDGE,"E1")])]}),"instanceName":"1"}),"instanceName":"1"}),"instanceName":"1"}),"instanceName":"1"});
            var Q997;
            Q997=makeQuery(id+"F12.opPattern","COPY",BODY,{"derivedFrom":makeQuery(id+"F10.opPattern","COPY",BODY,{"derivedFrom":makeQuery(id+"F7.opPattern","COPY",BODY,{"derivedFrom":makeQuery(id+"F6.opPattern","COPY",BODY,{"derivedFrom":makeQuery(id+"F2.opPattern","COPY",BODY,{"derivedFrom":makeQuery(id+"F1.opRevolve","SWEPT_BODY",BODY,{"disambiguationData":[OSD([sQuery(id+"F0.wireOp",EDGE,"E1")])]}),"instanceName":"1"}),"instanceName":"1"}),"instanceName":"1"}),"instanceName":"1"}),"instanceName":"1"});
            var Q998;
            Q998=makeQuery(id+"F12.opPattern","COPY",BODY,{"derivedFrom":makeQuery(id+"F10.opPattern","COPY",BODY,{"derivedFrom":makeQuery(id+"F7.opPattern","COPY",BODY,{"derivedFrom":makeQuery(id+"F6.opPattern","COPY",BODY,{"derivedFrom":makeQuery(id+"F3.opPattern","COPY",BODY,{"derivedFrom":makeQuery(id+"F2.opPattern","COPY",BODY,{"derivedFrom":makeQuery(id+"F1.opRevolve","SWEPT_BODY",BODY,{"disambiguationData":[OSD([sQuery(id+"F0.wireOp",EDGE,"E1")])]}),"instanceName":"1"}),"instanceName":"1"}),"instanceName":"1"}),"instanceName":"1"}),"instanceName":"1"}),"instanceName":"1"});
            var Q999;
            Q999=makeQuery(id+"F12.opPattern","COPY",BODY,{"derivedFrom":makeQuery(id+"F10.opPattern","COPY",BODY,{"derivedFrom":makeQuery(id+"F7.opPattern","COPY",BODY,{"derivedFrom":makeQuery(id+"F6.opPattern","COPY",BODY,{"derivedFrom":makeQuery(id+"F4.opPattern","COPY",BODY,{"derivedFrom":makeQuery(id+"F1.opRevolve","SWEPT_BODY",BODY,{"disambiguationData":[OSD([sQuery(id+"F0.wireOp",EDGE,"E1")])]}),"instanceName":"1"}),"instanceName":"1"}),"instanceName":"1"}),"instanceName":"1"}),"instanceName":"1"});
            var Q1000;
            Q1000=makeQuery(id+"F12.opPattern","COPY",BODY,{"derivedFrom":makeQuery(id+"F10.opPattern","COPY",BODY,{"derivedFrom":makeQuery(id+"F7.opPattern","COPY",BODY,{"derivedFrom":makeQuery(id+"F6.opPattern","COPY",BODY,{"derivedFrom":makeQuery(id+"F4.opPattern","COPY",BODY,{"derivedFrom":makeQuery(id+"F2.opPattern","COPY",BODY,{"derivedFrom":makeQuery(id+"F1.opRevolve","SWEPT_BODY",BODY,{"disambiguationData":[OSD([sQuery(id+"F0.wireOp",EDGE,"E1")])]}),"instanceName":"1"}),"instanceName":"1"}),"instanceName":"1"}),"instanceName":"1"}),"instanceName":"1"}),"instanceName":"1"});
            var Q1001;
            Q1001=makeQuery(id+"F12.opPattern","COPY",BODY,{"derivedFrom":makeQuery(id+"F10.opPattern","COPY",BODY,{"derivedFrom":makeQuery(id+"F7.opPattern","COPY",BODY,{"derivedFrom":makeQuery(id+"F6.opPattern","COPY",BODY,{"derivedFrom":makeQuery(id+"F4.opPattern","COPY",BODY,{"derivedFrom":makeQuery(id+"F3.opPattern","COPY",BODY,{"derivedFrom":makeQuery(id+"F2.opPattern","COPY",BODY,{"derivedFrom":makeQuery(id+"F1.opRevolve","SWEPT_BODY",BODY,{"disambiguationData":[OSD([sQuery(id+"F0.wireOp",EDGE,"E1")])]}),"instanceName":"1"}),"instanceName":"1"}),"instanceName":"1"}),"instanceName":"1"}),"instanceName":"1"}),"instanceName":"1"}),"instanceName":"1"});
            var Q1002;
            Q1002=makeQuery(id+"F12.opPattern","COPY",BODY,{"derivedFrom":makeQuery(id+"F10.opPattern","COPY",BODY,{"derivedFrom":makeQuery(id+"F7.opPattern","COPY",BODY,{"derivedFrom":makeQuery(id+"F6.opPattern","COPY",BODY,{"derivedFrom":makeQuery(id+"F5.opPattern","COPY",BODY,{"derivedFrom":makeQuery(id+"F1.opRevolve","SWEPT_BODY",BODY,{"disambiguationData":[OSD([sQuery(id+"F0.wireOp",EDGE,"E1")])]}),"instanceName":"1"}),"instanceName":"1"}),"instanceName":"1"}),"instanceName":"1"}),"instanceName":"1"});
            var Q1003;
            Q1003=makeQuery(id+"F12.opPattern","COPY",BODY,{"derivedFrom":makeQuery(id+"F10.opPattern","COPY",BODY,{"derivedFrom":makeQuery(id+"F7.opPattern","COPY",BODY,{"derivedFrom":makeQuery(id+"F6.opPattern","COPY",BODY,{"derivedFrom":makeQuery(id+"F5.opPattern","COPY",BODY,{"derivedFrom":makeQuery(id+"F2.opPattern","COPY",BODY,{"derivedFrom":makeQuery(id+"F1.opRevolve","SWEPT_BODY",BODY,{"disambiguationData":[OSD([sQuery(id+"F0.wireOp",EDGE,"E1")])]}),"instanceName":"1"}),"instanceName":"1"}),"instanceName":"1"}),"instanceName":"1"}),"instanceName":"1"}),"instanceName":"1"});
            var Q1004;
            Q1004=makeQuery(id+"F12.opPattern","COPY",BODY,{"derivedFrom":makeQuery(id+"F10.opPattern","COPY",BODY,{"derivedFrom":makeQuery(id+"F7.opPattern","COPY",BODY,{"derivedFrom":makeQuery(id+"F6.opPattern","COPY",BODY,{"derivedFrom":makeQuery(id+"F5.opPattern","COPY",BODY,{"derivedFrom":makeQuery(id+"F3.opPattern","COPY",BODY,{"derivedFrom":makeQuery(id+"F2.opPattern","COPY",BODY,{"derivedFrom":makeQuery(id+"F1.opRevolve","SWEPT_BODY",BODY,{"disambiguationData":[OSD([sQuery(id+"F0.wireOp",EDGE,"E1")])]}),"instanceName":"1"}),"instanceName":"1"}),"instanceName":"1"}),"instanceName":"1"}),"instanceName":"1"}),"instanceName":"1"}),"instanceName":"1"});
            var Q1005;
            Q1005=makeQuery(id+"F12.opPattern","COPY",BODY,{"derivedFrom":makeQuery(id+"F10.opPattern","COPY",BODY,{"derivedFrom":makeQuery(id+"F7.opPattern","COPY",BODY,{"derivedFrom":makeQuery(id+"F6.opPattern","COPY",BODY,{"derivedFrom":makeQuery(id+"F5.opPattern","COPY",BODY,{"derivedFrom":makeQuery(id+"F4.opPattern","COPY",BODY,{"derivedFrom":makeQuery(id+"F1.opRevolve","SWEPT_BODY",BODY,{"disambiguationData":[OSD([sQuery(id+"F0.wireOp",EDGE,"E1")])]}),"instanceName":"1"}),"instanceName":"1"}),"instanceName":"1"}),"instanceName":"1"}),"instanceName":"1"}),"instanceName":"1"});
            var Q1006;
            Q1006=makeQuery(id+"F12.opPattern","COPY",BODY,{"derivedFrom":makeQuery(id+"F10.opPattern","COPY",BODY,{"derivedFrom":makeQuery(id+"F7.opPattern","COPY",BODY,{"derivedFrom":makeQuery(id+"F6.opPattern","COPY",BODY,{"derivedFrom":makeQuery(id+"F5.opPattern","COPY",BODY,{"derivedFrom":makeQuery(id+"F4.opPattern","COPY",BODY,{"derivedFrom":makeQuery(id+"F2.opPattern","COPY",BODY,{"derivedFrom":makeQuery(id+"F1.opRevolve","SWEPT_BODY",BODY,{"disambiguationData":[OSD([sQuery(id+"F0.wireOp",EDGE,"E1")])]}),"instanceName":"1"}),"instanceName":"1"}),"instanceName":"1"}),"instanceName":"1"}),"instanceName":"1"}),"instanceName":"1"}),"instanceName":"1"});
            var Q1007;
            Q1007=makeQuery(id+"F12.opPattern","COPY",BODY,{"derivedFrom":makeQuery(id+"F10.opPattern","COPY",BODY,{"derivedFrom":makeQuery(id+"F7.opPattern","COPY",BODY,{"derivedFrom":makeQuery(id+"F6.opPattern","COPY",BODY,{"derivedFrom":makeQuery(id+"F5.opPattern","COPY",BODY,{"derivedFrom":makeQuery(id+"F4.opPattern","COPY",BODY,{"derivedFrom":makeQuery(id+"F3.opPattern","COPY",BODY,{"derivedFrom":makeQuery(id+"F2.opPattern","COPY",BODY,{"derivedFrom":makeQuery(id+"F1.opRevolve","SWEPT_BODY",BODY,{"disambiguationData":[OSD([sQuery(id+"F0.wireOp",EDGE,"E1")])]}),"instanceName":"1"}),"instanceName":"1"}),"instanceName":"1"}),"instanceName":"1"}),"instanceName":"1"}),"instanceName":"1"}),"instanceName":"1"}),"instanceName":"1"});
            var Q1008;
            Q1008=makeQuery(id+"F12.opPattern","COPY",BODY,{"derivedFrom":makeQuery(id+"F10.opPattern","COPY",BODY,{"derivedFrom":makeQuery(id+"F8.opPattern","COPY",BODY,{"derivedFrom":makeQuery(id+"F1.opRevolve","SWEPT_BODY",BODY,{"disambiguationData":[OSD([sQuery(id+"F0.wireOp",EDGE,"E1")])]}),"instanceName":"1"}),"instanceName":"1"}),"instanceName":"1"});
            var Q1009;
            Q1009=makeQuery(id+"F12.opPattern","COPY",BODY,{"derivedFrom":makeQuery(id+"F10.opPattern","COPY",BODY,{"derivedFrom":makeQuery(id+"F8.opPattern","COPY",BODY,{"derivedFrom":makeQuery(id+"F2.opPattern","COPY",BODY,{"derivedFrom":makeQuery(id+"F1.opRevolve","SWEPT_BODY",BODY,{"disambiguationData":[OSD([sQuery(id+"F0.wireOp",EDGE,"E1")])]}),"instanceName":"1"}),"instanceName":"1"}),"instanceName":"1"}),"instanceName":"1"});
            var Q1010;
            Q1010=makeQuery(id+"F12.opPattern","COPY",BODY,{"derivedFrom":makeQuery(id+"F10.opPattern","COPY",BODY,{"derivedFrom":makeQuery(id+"F8.opPattern","COPY",BODY,{"derivedFrom":makeQuery(id+"F3.opPattern","COPY",BODY,{"derivedFrom":makeQuery(id+"F2.opPattern","COPY",BODY,{"derivedFrom":makeQuery(id+"F1.opRevolve","SWEPT_BODY",BODY,{"disambiguationData":[OSD([sQuery(id+"F0.wireOp",EDGE,"E1")])]}),"instanceName":"1"}),"instanceName":"1"}),"instanceName":"1"}),"instanceName":"1"}),"instanceName":"1"});
            var Q1011;
            Q1011=makeQuery(id+"F12.opPattern","COPY",BODY,{"derivedFrom":makeQuery(id+"F10.opPattern","COPY",BODY,{"derivedFrom":makeQuery(id+"F8.opPattern","COPY",BODY,{"derivedFrom":makeQuery(id+"F4.opPattern","COPY",BODY,{"derivedFrom":makeQuery(id+"F1.opRevolve","SWEPT_BODY",BODY,{"disambiguationData":[OSD([sQuery(id+"F0.wireOp",EDGE,"E1")])]}),"instanceName":"1"}),"instanceName":"1"}),"instanceName":"1"}),"instanceName":"1"});
            var Q1012;
            Q1012=makeQuery(id+"F12.opPattern","COPY",BODY,{"derivedFrom":makeQuery(id+"F10.opPattern","COPY",BODY,{"derivedFrom":makeQuery(id+"F8.opPattern","COPY",BODY,{"derivedFrom":makeQuery(id+"F4.opPattern","COPY",BODY,{"derivedFrom":makeQuery(id+"F2.opPattern","COPY",BODY,{"derivedFrom":makeQuery(id+"F1.opRevolve","SWEPT_BODY",BODY,{"disambiguationData":[OSD([sQuery(id+"F0.wireOp",EDGE,"E1")])]}),"instanceName":"1"}),"instanceName":"1"}),"instanceName":"1"}),"instanceName":"1"}),"instanceName":"1"});
            var Q1013;
            Q1013=makeQuery(id+"F12.opPattern","COPY",BODY,{"derivedFrom":makeQuery(id+"F10.opPattern","COPY",BODY,{"derivedFrom":makeQuery(id+"F8.opPattern","COPY",BODY,{"derivedFrom":makeQuery(id+"F4.opPattern","COPY",BODY,{"derivedFrom":makeQuery(id+"F3.opPattern","COPY",BODY,{"derivedFrom":makeQuery(id+"F2.opPattern","COPY",BODY,{"derivedFrom":makeQuery(id+"F1.opRevolve","SWEPT_BODY",BODY,{"disambiguationData":[OSD([sQuery(id+"F0.wireOp",EDGE,"E1")])]}),"instanceName":"1"}),"instanceName":"1"}),"instanceName":"1"}),"instanceName":"1"}),"instanceName":"1"}),"instanceName":"1"});
            var Q1014;
            Q1014=makeQuery(id+"F12.opPattern","COPY",BODY,{"derivedFrom":makeQuery(id+"F10.opPattern","COPY",BODY,{"derivedFrom":makeQuery(id+"F8.opPattern","COPY",BODY,{"derivedFrom":makeQuery(id+"F5.opPattern","COPY",BODY,{"derivedFrom":makeQuery(id+"F1.opRevolve","SWEPT_BODY",BODY,{"disambiguationData":[OSD([sQuery(id+"F0.wireOp",EDGE,"E1")])]}),"instanceName":"1"}),"instanceName":"1"}),"instanceName":"1"}),"instanceName":"1"});
            var Q1015;
            Q1015=makeQuery(id+"F12.opPattern","COPY",BODY,{"derivedFrom":makeQuery(id+"F10.opPattern","COPY",BODY,{"derivedFrom":makeQuery(id+"F8.opPattern","COPY",BODY,{"derivedFrom":makeQuery(id+"F5.opPattern","COPY",BODY,{"derivedFrom":makeQuery(id+"F2.opPattern","COPY",BODY,{"derivedFrom":makeQuery(id+"F1.opRevolve","SWEPT_BODY",BODY,{"disambiguationData":[OSD([sQuery(id+"F0.wireOp",EDGE,"E1")])]}),"instanceName":"1"}),"instanceName":"1"}),"instanceName":"1"}),"instanceName":"1"}),"instanceName":"1"});
            var Q1016;
            Q1016=makeQuery(id+"F12.opPattern","COPY",BODY,{"derivedFrom":makeQuery(id+"F10.opPattern","COPY",BODY,{"derivedFrom":makeQuery(id+"F8.opPattern","COPY",BODY,{"derivedFrom":makeQuery(id+"F5.opPattern","COPY",BODY,{"derivedFrom":makeQuery(id+"F3.opPattern","COPY",BODY,{"derivedFrom":makeQuery(id+"F2.opPattern","COPY",BODY,{"derivedFrom":makeQuery(id+"F1.opRevolve","SWEPT_BODY",BODY,{"disambiguationData":[OSD([sQuery(id+"F0.wireOp",EDGE,"E1")])]}),"instanceName":"1"}),"instanceName":"1"}),"instanceName":"1"}),"instanceName":"1"}),"instanceName":"1"}),"instanceName":"1"});
            var Q1017;
            Q1017=makeQuery(id+"F12.opPattern","COPY",BODY,{"derivedFrom":makeQuery(id+"F10.opPattern","COPY",BODY,{"derivedFrom":makeQuery(id+"F8.opPattern","COPY",BODY,{"derivedFrom":makeQuery(id+"F5.opPattern","COPY",BODY,{"derivedFrom":makeQuery(id+"F4.opPattern","COPY",BODY,{"derivedFrom":makeQuery(id+"F1.opRevolve","SWEPT_BODY",BODY,{"disambiguationData":[OSD([sQuery(id+"F0.wireOp",EDGE,"E1")])]}),"instanceName":"1"}),"instanceName":"1"}),"instanceName":"1"}),"instanceName":"1"}),"instanceName":"1"});
            var Q1018;
            Q1018=makeQuery(id+"F12.opPattern","COPY",BODY,{"derivedFrom":makeQuery(id+"F10.opPattern","COPY",BODY,{"derivedFrom":makeQuery(id+"F8.opPattern","COPY",BODY,{"derivedFrom":makeQuery(id+"F5.opPattern","COPY",BODY,{"derivedFrom":makeQuery(id+"F4.opPattern","COPY",BODY,{"derivedFrom":makeQuery(id+"F2.opPattern","COPY",BODY,{"derivedFrom":makeQuery(id+"F1.opRevolve","SWEPT_BODY",BODY,{"disambiguationData":[OSD([sQuery(id+"F0.wireOp",EDGE,"E1")])]}),"instanceName":"1"}),"instanceName":"1"}),"instanceName":"1"}),"instanceName":"1"}),"instanceName":"1"}),"instanceName":"1"});
            var Q1019;
            Q1019=makeQuery(id+"F12.opPattern","COPY",BODY,{"derivedFrom":makeQuery(id+"F10.opPattern","COPY",BODY,{"derivedFrom":makeQuery(id+"F8.opPattern","COPY",BODY,{"derivedFrom":makeQuery(id+"F5.opPattern","COPY",BODY,{"derivedFrom":makeQuery(id+"F4.opPattern","COPY",BODY,{"derivedFrom":makeQuery(id+"F3.opPattern","COPY",BODY,{"derivedFrom":makeQuery(id+"F2.opPattern","COPY",BODY,{"derivedFrom":makeQuery(id+"F1.opRevolve","SWEPT_BODY",BODY,{"disambiguationData":[OSD([sQuery(id+"F0.wireOp",EDGE,"E1")])]}),"instanceName":"1"}),"instanceName":"1"}),"instanceName":"1"}),"instanceName":"1"}),"instanceName":"1"}),"instanceName":"1"}),"instanceName":"1"});
            var Q1020;
            Q1020=makeQuery(id+"F12.opPattern","COPY",BODY,{"derivedFrom":makeQuery(id+"F10.opPattern","COPY",BODY,{"derivedFrom":makeQuery(id+"F8.opPattern","COPY",BODY,{"derivedFrom":makeQuery(id+"F6.opPattern","COPY",BODY,{"derivedFrom":makeQuery(id+"F1.opRevolve","SWEPT_BODY",BODY,{"disambiguationData":[OSD([sQuery(id+"F0.wireOp",EDGE,"E1")])]}),"instanceName":"1"}),"instanceName":"1"}),"instanceName":"1"}),"instanceName":"1"});
            var Q1021;
            Q1021=makeQuery(id+"F12.opPattern","COPY",BODY,{"derivedFrom":makeQuery(id+"F10.opPattern","COPY",BODY,{"derivedFrom":makeQuery(id+"F8.opPattern","COPY",BODY,{"derivedFrom":makeQuery(id+"F6.opPattern","COPY",BODY,{"derivedFrom":makeQuery(id+"F2.opPattern","COPY",BODY,{"derivedFrom":makeQuery(id+"F1.opRevolve","SWEPT_BODY",BODY,{"disambiguationData":[OSD([sQuery(id+"F0.wireOp",EDGE,"E1")])]}),"instanceName":"1"}),"instanceName":"1"}),"instanceName":"1"}),"instanceName":"1"}),"instanceName":"1"});
            var Q1022;
            Q1022=makeQuery(id+"F12.opPattern","COPY",BODY,{"derivedFrom":makeQuery(id+"F10.opPattern","COPY",BODY,{"derivedFrom":makeQuery(id+"F8.opPattern","COPY",BODY,{"derivedFrom":makeQuery(id+"F6.opPattern","COPY",BODY,{"derivedFrom":makeQuery(id+"F3.opPattern","COPY",BODY,{"derivedFrom":makeQuery(id+"F2.opPattern","COPY",BODY,{"derivedFrom":makeQuery(id+"F1.opRevolve","SWEPT_BODY",BODY,{"disambiguationData":[OSD([sQuery(id+"F0.wireOp",EDGE,"E1")])]}),"instanceName":"1"}),"instanceName":"1"}),"instanceName":"1"}),"instanceName":"1"}),"instanceName":"1"}),"instanceName":"1"});
            var Q1023;
            Q1023=makeQuery(id+"F12.opPattern","COPY",BODY,{"derivedFrom":makeQuery(id+"F10.opPattern","COPY",BODY,{"derivedFrom":makeQuery(id+"F8.opPattern","COPY",BODY,{"derivedFrom":makeQuery(id+"F6.opPattern","COPY",BODY,{"derivedFrom":makeQuery(id+"F4.opPattern","COPY",BODY,{"derivedFrom":makeQuery(id+"F1.opRevolve","SWEPT_BODY",BODY,{"disambiguationData":[OSD([sQuery(id+"F0.wireOp",EDGE,"E1")])]}),"instanceName":"1"}),"instanceName":"1"}),"instanceName":"1"}),"instanceName":"1"}),"instanceName":"1"});
            var Q1024;
            Q1024=makeQuery(id+"F12.opPattern","COPY",BODY,{"derivedFrom":makeQuery(id+"F10.opPattern","COPY",BODY,{"derivedFrom":makeQuery(id+"F8.opPattern","COPY",BODY,{"derivedFrom":makeQuery(id+"F6.opPattern","COPY",BODY,{"derivedFrom":makeQuery(id+"F4.opPattern","COPY",BODY,{"derivedFrom":makeQuery(id+"F2.opPattern","COPY",BODY,{"derivedFrom":makeQuery(id+"F1.opRevolve","SWEPT_BODY",BODY,{"disambiguationData":[OSD([sQuery(id+"F0.wireOp",EDGE,"E1")])]}),"instanceName":"1"}),"instanceName":"1"}),"instanceName":"1"}),"instanceName":"1"}),"instanceName":"1"}),"instanceName":"1"});
            var Q1025;
            Q1025=makeQuery(id+"F12.opPattern","COPY",BODY,{"derivedFrom":makeQuery(id+"F10.opPattern","COPY",BODY,{"derivedFrom":makeQuery(id+"F8.opPattern","COPY",BODY,{"derivedFrom":makeQuery(id+"F6.opPattern","COPY",BODY,{"derivedFrom":makeQuery(id+"F4.opPattern","COPY",BODY,{"derivedFrom":makeQuery(id+"F3.opPattern","COPY",BODY,{"derivedFrom":makeQuery(id+"F2.opPattern","COPY",BODY,{"derivedFrom":makeQuery(id+"F1.opRevolve","SWEPT_BODY",BODY,{"disambiguationData":[OSD([sQuery(id+"F0.wireOp",EDGE,"E1")])]}),"instanceName":"1"}),"instanceName":"1"}),"instanceName":"1"}),"instanceName":"1"}),"instanceName":"1"}),"instanceName":"1"}),"instanceName":"1"});
            var Q1026;
            Q1026=makeQuery(id+"F12.opPattern","COPY",BODY,{"derivedFrom":makeQuery(id+"F10.opPattern","COPY",BODY,{"derivedFrom":makeQuery(id+"F8.opPattern","COPY",BODY,{"derivedFrom":makeQuery(id+"F6.opPattern","COPY",BODY,{"derivedFrom":makeQuery(id+"F5.opPattern","COPY",BODY,{"derivedFrom":makeQuery(id+"F1.opRevolve","SWEPT_BODY",BODY,{"disambiguationData":[OSD([sQuery(id+"F0.wireOp",EDGE,"E1")])]}),"instanceName":"1"}),"instanceName":"1"}),"instanceName":"1"}),"instanceName":"1"}),"instanceName":"1"});
            var Q1027;
            Q1027=makeQuery(id+"F12.opPattern","COPY",BODY,{"derivedFrom":makeQuery(id+"F10.opPattern","COPY",BODY,{"derivedFrom":makeQuery(id+"F8.opPattern","COPY",BODY,{"derivedFrom":makeQuery(id+"F6.opPattern","COPY",BODY,{"derivedFrom":makeQuery(id+"F5.opPattern","COPY",BODY,{"derivedFrom":makeQuery(id+"F2.opPattern","COPY",BODY,{"derivedFrom":makeQuery(id+"F1.opRevolve","SWEPT_BODY",BODY,{"disambiguationData":[OSD([sQuery(id+"F0.wireOp",EDGE,"E1")])]}),"instanceName":"1"}),"instanceName":"1"}),"instanceName":"1"}),"instanceName":"1"}),"instanceName":"1"}),"instanceName":"1"});
            var Q1028;
            Q1028=makeQuery(id+"F12.opPattern","COPY",BODY,{"derivedFrom":makeQuery(id+"F10.opPattern","COPY",BODY,{"derivedFrom":makeQuery(id+"F8.opPattern","COPY",BODY,{"derivedFrom":makeQuery(id+"F6.opPattern","COPY",BODY,{"derivedFrom":makeQuery(id+"F5.opPattern","COPY",BODY,{"derivedFrom":makeQuery(id+"F3.opPattern","COPY",BODY,{"derivedFrom":makeQuery(id+"F2.opPattern","COPY",BODY,{"derivedFrom":makeQuery(id+"F1.opRevolve","SWEPT_BODY",BODY,{"disambiguationData":[OSD([sQuery(id+"F0.wireOp",EDGE,"E1")])]}),"instanceName":"1"}),"instanceName":"1"}),"instanceName":"1"}),"instanceName":"1"}),"instanceName":"1"}),"instanceName":"1"}),"instanceName":"1"});
            var Q1029;
            Q1029=makeQuery(id+"F12.opPattern","COPY",BODY,{"derivedFrom":makeQuery(id+"F10.opPattern","COPY",BODY,{"derivedFrom":makeQuery(id+"F8.opPattern","COPY",BODY,{"derivedFrom":makeQuery(id+"F6.opPattern","COPY",BODY,{"derivedFrom":makeQuery(id+"F5.opPattern","COPY",BODY,{"derivedFrom":makeQuery(id+"F4.opPattern","COPY",BODY,{"derivedFrom":makeQuery(id+"F1.opRevolve","SWEPT_BODY",BODY,{"disambiguationData":[OSD([sQuery(id+"F0.wireOp",EDGE,"E1")])]}),"instanceName":"1"}),"instanceName":"1"}),"instanceName":"1"}),"instanceName":"1"}),"instanceName":"1"}),"instanceName":"1"});
            var Q1030;
            Q1030=makeQuery(id+"F12.opPattern","COPY",BODY,{"derivedFrom":makeQuery(id+"F10.opPattern","COPY",BODY,{"derivedFrom":makeQuery(id+"F8.opPattern","COPY",BODY,{"derivedFrom":makeQuery(id+"F6.opPattern","COPY",BODY,{"derivedFrom":makeQuery(id+"F5.opPattern","COPY",BODY,{"derivedFrom":makeQuery(id+"F4.opPattern","COPY",BODY,{"derivedFrom":makeQuery(id+"F2.opPattern","COPY",BODY,{"derivedFrom":makeQuery(id+"F1.opRevolve","SWEPT_BODY",BODY,{"disambiguationData":[OSD([sQuery(id+"F0.wireOp",EDGE,"E1")])]}),"instanceName":"1"}),"instanceName":"1"}),"instanceName":"1"}),"instanceName":"1"}),"instanceName":"1"}),"instanceName":"1"}),"instanceName":"1"});
            var Q1031;
            Q1031=makeQuery(id+"F12.opPattern","COPY",BODY,{"derivedFrom":makeQuery(id+"F10.opPattern","COPY",BODY,{"derivedFrom":makeQuery(id+"F8.opPattern","COPY",BODY,{"derivedFrom":makeQuery(id+"F6.opPattern","COPY",BODY,{"derivedFrom":makeQuery(id+"F5.opPattern","COPY",BODY,{"derivedFrom":makeQuery(id+"F4.opPattern","COPY",BODY,{"derivedFrom":makeQuery(id+"F3.opPattern","COPY",BODY,{"derivedFrom":makeQuery(id+"F2.opPattern","COPY",BODY,{"derivedFrom":makeQuery(id+"F1.opRevolve","SWEPT_BODY",BODY,{"disambiguationData":[OSD([sQuery(id+"F0.wireOp",EDGE,"E1")])]}),"instanceName":"1"}),"instanceName":"1"}),"instanceName":"1"}),"instanceName":"1"}),"instanceName":"1"}),"instanceName":"1"}),"instanceName":"1"}),"instanceName":"1"});
            var Q1032;
            Q1032=makeQuery(id+"F12.opPattern","COPY",BODY,{"derivedFrom":makeQuery(id+"F10.opPattern","COPY",BODY,{"derivedFrom":makeQuery(id+"F8.opPattern","COPY",BODY,{"derivedFrom":makeQuery(id+"F7.opPattern","COPY",BODY,{"derivedFrom":makeQuery(id+"F1.opRevolve","SWEPT_BODY",BODY,{"disambiguationData":[OSD([sQuery(id+"F0.wireOp",EDGE,"E1")])]}),"instanceName":"1"}),"instanceName":"1"}),"instanceName":"1"}),"instanceName":"1"});
            var Q1033;
            Q1033=makeQuery(id+"F12.opPattern","COPY",BODY,{"derivedFrom":makeQuery(id+"F10.opPattern","COPY",BODY,{"derivedFrom":makeQuery(id+"F8.opPattern","COPY",BODY,{"derivedFrom":makeQuery(id+"F7.opPattern","COPY",BODY,{"derivedFrom":makeQuery(id+"F2.opPattern","COPY",BODY,{"derivedFrom":makeQuery(id+"F1.opRevolve","SWEPT_BODY",BODY,{"disambiguationData":[OSD([sQuery(id+"F0.wireOp",EDGE,"E1")])]}),"instanceName":"1"}),"instanceName":"1"}),"instanceName":"1"}),"instanceName":"1"}),"instanceName":"1"});
            var Q1034;
            Q1034=makeQuery(id+"F12.opPattern","COPY",BODY,{"derivedFrom":makeQuery(id+"F10.opPattern","COPY",BODY,{"derivedFrom":makeQuery(id+"F8.opPattern","COPY",BODY,{"derivedFrom":makeQuery(id+"F7.opPattern","COPY",BODY,{"derivedFrom":makeQuery(id+"F3.opPattern","COPY",BODY,{"derivedFrom":makeQuery(id+"F2.opPattern","COPY",BODY,{"derivedFrom":makeQuery(id+"F1.opRevolve","SWEPT_BODY",BODY,{"disambiguationData":[OSD([sQuery(id+"F0.wireOp",EDGE,"E1")])]}),"instanceName":"1"}),"instanceName":"1"}),"instanceName":"1"}),"instanceName":"1"}),"instanceName":"1"}),"instanceName":"1"});
            var Q1035;
            Q1035=makeQuery(id+"F12.opPattern","COPY",BODY,{"derivedFrom":makeQuery(id+"F10.opPattern","COPY",BODY,{"derivedFrom":makeQuery(id+"F8.opPattern","COPY",BODY,{"derivedFrom":makeQuery(id+"F7.opPattern","COPY",BODY,{"derivedFrom":makeQuery(id+"F4.opPattern","COPY",BODY,{"derivedFrom":makeQuery(id+"F1.opRevolve","SWEPT_BODY",BODY,{"disambiguationData":[OSD([sQuery(id+"F0.wireOp",EDGE,"E1")])]}),"instanceName":"1"}),"instanceName":"1"}),"instanceName":"1"}),"instanceName":"1"}),"instanceName":"1"});
            var Q1036;
            Q1036=makeQuery(id+"F12.opPattern","COPY",BODY,{"derivedFrom":makeQuery(id+"F10.opPattern","COPY",BODY,{"derivedFrom":makeQuery(id+"F8.opPattern","COPY",BODY,{"derivedFrom":makeQuery(id+"F7.opPattern","COPY",BODY,{"derivedFrom":makeQuery(id+"F4.opPattern","COPY",BODY,{"derivedFrom":makeQuery(id+"F2.opPattern","COPY",BODY,{"derivedFrom":makeQuery(id+"F1.opRevolve","SWEPT_BODY",BODY,{"disambiguationData":[OSD([sQuery(id+"F0.wireOp",EDGE,"E1")])]}),"instanceName":"1"}),"instanceName":"1"}),"instanceName":"1"}),"instanceName":"1"}),"instanceName":"1"}),"instanceName":"1"});
            var Q1037;
            Q1037=makeQuery(id+"F12.opPattern","COPY",BODY,{"derivedFrom":makeQuery(id+"F10.opPattern","COPY",BODY,{"derivedFrom":makeQuery(id+"F8.opPattern","COPY",BODY,{"derivedFrom":makeQuery(id+"F7.opPattern","COPY",BODY,{"derivedFrom":makeQuery(id+"F4.opPattern","COPY",BODY,{"derivedFrom":makeQuery(id+"F3.opPattern","COPY",BODY,{"derivedFrom":makeQuery(id+"F2.opPattern","COPY",BODY,{"derivedFrom":makeQuery(id+"F1.opRevolve","SWEPT_BODY",BODY,{"disambiguationData":[OSD([sQuery(id+"F0.wireOp",EDGE,"E1")])]}),"instanceName":"1"}),"instanceName":"1"}),"instanceName":"1"}),"instanceName":"1"}),"instanceName":"1"}),"instanceName":"1"}),"instanceName":"1"});
            var Q1038;
            Q1038=makeQuery(id+"F12.opPattern","COPY",BODY,{"derivedFrom":makeQuery(id+"F10.opPattern","COPY",BODY,{"derivedFrom":makeQuery(id+"F8.opPattern","COPY",BODY,{"derivedFrom":makeQuery(id+"F7.opPattern","COPY",BODY,{"derivedFrom":makeQuery(id+"F5.opPattern","COPY",BODY,{"derivedFrom":makeQuery(id+"F1.opRevolve","SWEPT_BODY",BODY,{"disambiguationData":[OSD([sQuery(id+"F0.wireOp",EDGE,"E1")])]}),"instanceName":"1"}),"instanceName":"1"}),"instanceName":"1"}),"instanceName":"1"}),"instanceName":"1"});
            var Q1039;
            Q1039=makeQuery(id+"F12.opPattern","COPY",BODY,{"derivedFrom":makeQuery(id+"F10.opPattern","COPY",BODY,{"derivedFrom":makeQuery(id+"F8.opPattern","COPY",BODY,{"derivedFrom":makeQuery(id+"F7.opPattern","COPY",BODY,{"derivedFrom":makeQuery(id+"F5.opPattern","COPY",BODY,{"derivedFrom":makeQuery(id+"F2.opPattern","COPY",BODY,{"derivedFrom":makeQuery(id+"F1.opRevolve","SWEPT_BODY",BODY,{"disambiguationData":[OSD([sQuery(id+"F0.wireOp",EDGE,"E1")])]}),"instanceName":"1"}),"instanceName":"1"}),"instanceName":"1"}),"instanceName":"1"}),"instanceName":"1"}),"instanceName":"1"});
            var Q1040;
            Q1040=makeQuery(id+"F12.opPattern","COPY",BODY,{"derivedFrom":makeQuery(id+"F10.opPattern","COPY",BODY,{"derivedFrom":makeQuery(id+"F8.opPattern","COPY",BODY,{"derivedFrom":makeQuery(id+"F7.opPattern","COPY",BODY,{"derivedFrom":makeQuery(id+"F5.opPattern","COPY",BODY,{"derivedFrom":makeQuery(id+"F3.opPattern","COPY",BODY,{"derivedFrom":makeQuery(id+"F2.opPattern","COPY",BODY,{"derivedFrom":makeQuery(id+"F1.opRevolve","SWEPT_BODY",BODY,{"disambiguationData":[OSD([sQuery(id+"F0.wireOp",EDGE,"E1")])]}),"instanceName":"1"}),"instanceName":"1"}),"instanceName":"1"}),"instanceName":"1"}),"instanceName":"1"}),"instanceName":"1"}),"instanceName":"1"});
            var Q1041;
            Q1041=makeQuery(id+"F12.opPattern","COPY",BODY,{"derivedFrom":makeQuery(id+"F10.opPattern","COPY",BODY,{"derivedFrom":makeQuery(id+"F8.opPattern","COPY",BODY,{"derivedFrom":makeQuery(id+"F7.opPattern","COPY",BODY,{"derivedFrom":makeQuery(id+"F5.opPattern","COPY",BODY,{"derivedFrom":makeQuery(id+"F4.opPattern","COPY",BODY,{"derivedFrom":makeQuery(id+"F1.opRevolve","SWEPT_BODY",BODY,{"disambiguationData":[OSD([sQuery(id+"F0.wireOp",EDGE,"E1")])]}),"instanceName":"1"}),"instanceName":"1"}),"instanceName":"1"}),"instanceName":"1"}),"instanceName":"1"}),"instanceName":"1"});
            var Q1042;
            Q1042=makeQuery(id+"F12.opPattern","COPY",BODY,{"derivedFrom":makeQuery(id+"F10.opPattern","COPY",BODY,{"derivedFrom":makeQuery(id+"F8.opPattern","COPY",BODY,{"derivedFrom":makeQuery(id+"F7.opPattern","COPY",BODY,{"derivedFrom":makeQuery(id+"F5.opPattern","COPY",BODY,{"derivedFrom":makeQuery(id+"F4.opPattern","COPY",BODY,{"derivedFrom":makeQuery(id+"F2.opPattern","COPY",BODY,{"derivedFrom":makeQuery(id+"F1.opRevolve","SWEPT_BODY",BODY,{"disambiguationData":[OSD([sQuery(id+"F0.wireOp",EDGE,"E1")])]}),"instanceName":"1"}),"instanceName":"1"}),"instanceName":"1"}),"instanceName":"1"}),"instanceName":"1"}),"instanceName":"1"}),"instanceName":"1"});
            var Q1043;
            Q1043=makeQuery(id+"F12.opPattern","COPY",BODY,{"derivedFrom":makeQuery(id+"F10.opPattern","COPY",BODY,{"derivedFrom":makeQuery(id+"F8.opPattern","COPY",BODY,{"derivedFrom":makeQuery(id+"F7.opPattern","COPY",BODY,{"derivedFrom":makeQuery(id+"F5.opPattern","COPY",BODY,{"derivedFrom":makeQuery(id+"F4.opPattern","COPY",BODY,{"derivedFrom":makeQuery(id+"F3.opPattern","COPY",BODY,{"derivedFrom":makeQuery(id+"F2.opPattern","COPY",BODY,{"derivedFrom":makeQuery(id+"F1.opRevolve","SWEPT_BODY",BODY,{"disambiguationData":[OSD([sQuery(id+"F0.wireOp",EDGE,"E1")])]}),"instanceName":"1"}),"instanceName":"1"}),"instanceName":"1"}),"instanceName":"1"}),"instanceName":"1"}),"instanceName":"1"}),"instanceName":"1"}),"instanceName":"1"});
            var Q1044;
            Q1044=makeQuery(id+"F12.opPattern","COPY",BODY,{"derivedFrom":makeQuery(id+"F10.opPattern","COPY",BODY,{"derivedFrom":makeQuery(id+"F8.opPattern","COPY",BODY,{"derivedFrom":makeQuery(id+"F7.opPattern","COPY",BODY,{"derivedFrom":makeQuery(id+"F6.opPattern","COPY",BODY,{"derivedFrom":makeQuery(id+"F1.opRevolve","SWEPT_BODY",BODY,{"disambiguationData":[OSD([sQuery(id+"F0.wireOp",EDGE,"E1")])]}),"instanceName":"1"}),"instanceName":"1"}),"instanceName":"1"}),"instanceName":"1"}),"instanceName":"1"});
            var Q1045;
            Q1045=makeQuery(id+"F12.opPattern","COPY",BODY,{"derivedFrom":makeQuery(id+"F10.opPattern","COPY",BODY,{"derivedFrom":makeQuery(id+"F8.opPattern","COPY",BODY,{"derivedFrom":makeQuery(id+"F7.opPattern","COPY",BODY,{"derivedFrom":makeQuery(id+"F6.opPattern","COPY",BODY,{"derivedFrom":makeQuery(id+"F2.opPattern","COPY",BODY,{"derivedFrom":makeQuery(id+"F1.opRevolve","SWEPT_BODY",BODY,{"disambiguationData":[OSD([sQuery(id+"F0.wireOp",EDGE,"E1")])]}),"instanceName":"1"}),"instanceName":"1"}),"instanceName":"1"}),"instanceName":"1"}),"instanceName":"1"}),"instanceName":"1"});
            var Q1046;
            Q1046=makeQuery(id+"F12.opPattern","COPY",BODY,{"derivedFrom":makeQuery(id+"F10.opPattern","COPY",BODY,{"derivedFrom":makeQuery(id+"F8.opPattern","COPY",BODY,{"derivedFrom":makeQuery(id+"F7.opPattern","COPY",BODY,{"derivedFrom":makeQuery(id+"F6.opPattern","COPY",BODY,{"derivedFrom":makeQuery(id+"F3.opPattern","COPY",BODY,{"derivedFrom":makeQuery(id+"F2.opPattern","COPY",BODY,{"derivedFrom":makeQuery(id+"F1.opRevolve","SWEPT_BODY",BODY,{"disambiguationData":[OSD([sQuery(id+"F0.wireOp",EDGE,"E1")])]}),"instanceName":"1"}),"instanceName":"1"}),"instanceName":"1"}),"instanceName":"1"}),"instanceName":"1"}),"instanceName":"1"}),"instanceName":"1"});
            var Q1047;
            Q1047=makeQuery(id+"F12.opPattern","COPY",BODY,{"derivedFrom":makeQuery(id+"F10.opPattern","COPY",BODY,{"derivedFrom":makeQuery(id+"F8.opPattern","COPY",BODY,{"derivedFrom":makeQuery(id+"F7.opPattern","COPY",BODY,{"derivedFrom":makeQuery(id+"F6.opPattern","COPY",BODY,{"derivedFrom":makeQuery(id+"F4.opPattern","COPY",BODY,{"derivedFrom":makeQuery(id+"F1.opRevolve","SWEPT_BODY",BODY,{"disambiguationData":[OSD([sQuery(id+"F0.wireOp",EDGE,"E1")])]}),"instanceName":"1"}),"instanceName":"1"}),"instanceName":"1"}),"instanceName":"1"}),"instanceName":"1"}),"instanceName":"1"});
            var Q1048;
            Q1048=makeQuery(id+"F12.opPattern","COPY",BODY,{"derivedFrom":makeQuery(id+"F10.opPattern","COPY",BODY,{"derivedFrom":makeQuery(id+"F8.opPattern","COPY",BODY,{"derivedFrom":makeQuery(id+"F7.opPattern","COPY",BODY,{"derivedFrom":makeQuery(id+"F6.opPattern","COPY",BODY,{"derivedFrom":makeQuery(id+"F4.opPattern","COPY",BODY,{"derivedFrom":makeQuery(id+"F2.opPattern","COPY",BODY,{"derivedFrom":makeQuery(id+"F1.opRevolve","SWEPT_BODY",BODY,{"disambiguationData":[OSD([sQuery(id+"F0.wireOp",EDGE,"E1")])]}),"instanceName":"1"}),"instanceName":"1"}),"instanceName":"1"}),"instanceName":"1"}),"instanceName":"1"}),"instanceName":"1"}),"instanceName":"1"});
            var Q1049;
            Q1049=makeQuery(id+"F12.opPattern","COPY",BODY,{"derivedFrom":makeQuery(id+"F10.opPattern","COPY",BODY,{"derivedFrom":makeQuery(id+"F8.opPattern","COPY",BODY,{"derivedFrom":makeQuery(id+"F7.opPattern","COPY",BODY,{"derivedFrom":makeQuery(id+"F6.opPattern","COPY",BODY,{"derivedFrom":makeQuery(id+"F4.opPattern","COPY",BODY,{"derivedFrom":makeQuery(id+"F3.opPattern","COPY",BODY,{"derivedFrom":makeQuery(id+"F2.opPattern","COPY",BODY,{"derivedFrom":makeQuery(id+"F1.opRevolve","SWEPT_BODY",BODY,{"disambiguationData":[OSD([sQuery(id+"F0.wireOp",EDGE,"E1")])]}),"instanceName":"1"}),"instanceName":"1"}),"instanceName":"1"}),"instanceName":"1"}),"instanceName":"1"}),"instanceName":"1"}),"instanceName":"1"}),"instanceName":"1"});
            var Q1050;
            Q1050=makeQuery(id+"F12.opPattern","COPY",BODY,{"derivedFrom":makeQuery(id+"F10.opPattern","COPY",BODY,{"derivedFrom":makeQuery(id+"F8.opPattern","COPY",BODY,{"derivedFrom":makeQuery(id+"F7.opPattern","COPY",BODY,{"derivedFrom":makeQuery(id+"F6.opPattern","COPY",BODY,{"derivedFrom":makeQuery(id+"F5.opPattern","COPY",BODY,{"derivedFrom":makeQuery(id+"F1.opRevolve","SWEPT_BODY",BODY,{"disambiguationData":[OSD([sQuery(id+"F0.wireOp",EDGE,"E1")])]}),"instanceName":"1"}),"instanceName":"1"}),"instanceName":"1"}),"instanceName":"1"}),"instanceName":"1"}),"instanceName":"1"});
            var Q1051;
            Q1051=makeQuery(id+"F12.opPattern","COPY",BODY,{"derivedFrom":makeQuery(id+"F10.opPattern","COPY",BODY,{"derivedFrom":makeQuery(id+"F8.opPattern","COPY",BODY,{"derivedFrom":makeQuery(id+"F7.opPattern","COPY",BODY,{"derivedFrom":makeQuery(id+"F6.opPattern","COPY",BODY,{"derivedFrom":makeQuery(id+"F5.opPattern","COPY",BODY,{"derivedFrom":makeQuery(id+"F2.opPattern","COPY",BODY,{"derivedFrom":makeQuery(id+"F1.opRevolve","SWEPT_BODY",BODY,{"disambiguationData":[OSD([sQuery(id+"F0.wireOp",EDGE,"E1")])]}),"instanceName":"1"}),"instanceName":"1"}),"instanceName":"1"}),"instanceName":"1"}),"instanceName":"1"}),"instanceName":"1"}),"instanceName":"1"});
            var Q1052;
            Q1052=makeQuery(id+"F12.opPattern","COPY",BODY,{"derivedFrom":makeQuery(id+"F10.opPattern","COPY",BODY,{"derivedFrom":makeQuery(id+"F8.opPattern","COPY",BODY,{"derivedFrom":makeQuery(id+"F7.opPattern","COPY",BODY,{"derivedFrom":makeQuery(id+"F6.opPattern","COPY",BODY,{"derivedFrom":makeQuery(id+"F5.opPattern","COPY",BODY,{"derivedFrom":makeQuery(id+"F3.opPattern","COPY",BODY,{"derivedFrom":makeQuery(id+"F2.opPattern","COPY",BODY,{"derivedFrom":makeQuery(id+"F1.opRevolve","SWEPT_BODY",BODY,{"disambiguationData":[OSD([sQuery(id+"F0.wireOp",EDGE,"E1")])]}),"instanceName":"1"}),"instanceName":"1"}),"instanceName":"1"}),"instanceName":"1"}),"instanceName":"1"}),"instanceName":"1"}),"instanceName":"1"}),"instanceName":"1"});
            var Q1053;
            Q1053=makeQuery(id+"F12.opPattern","COPY",BODY,{"derivedFrom":makeQuery(id+"F10.opPattern","COPY",BODY,{"derivedFrom":makeQuery(id+"F8.opPattern","COPY",BODY,{"derivedFrom":makeQuery(id+"F7.opPattern","COPY",BODY,{"derivedFrom":makeQuery(id+"F6.opPattern","COPY",BODY,{"derivedFrom":makeQuery(id+"F5.opPattern","COPY",BODY,{"derivedFrom":makeQuery(id+"F4.opPattern","COPY",BODY,{"derivedFrom":makeQuery(id+"F1.opRevolve","SWEPT_BODY",BODY,{"disambiguationData":[OSD([sQuery(id+"F0.wireOp",EDGE,"E1")])]}),"instanceName":"1"}),"instanceName":"1"}),"instanceName":"1"}),"instanceName":"1"}),"instanceName":"1"}),"instanceName":"1"}),"instanceName":"1"});
            var Q1054;
            Q1054=makeQuery(id+"F12.opPattern","COPY",BODY,{"derivedFrom":makeQuery(id+"F10.opPattern","COPY",BODY,{"derivedFrom":makeQuery(id+"F8.opPattern","COPY",BODY,{"derivedFrom":makeQuery(id+"F7.opPattern","COPY",BODY,{"derivedFrom":makeQuery(id+"F6.opPattern","COPY",BODY,{"derivedFrom":makeQuery(id+"F5.opPattern","COPY",BODY,{"derivedFrom":makeQuery(id+"F4.opPattern","COPY",BODY,{"derivedFrom":makeQuery(id+"F2.opPattern","COPY",BODY,{"derivedFrom":makeQuery(id+"F1.opRevolve","SWEPT_BODY",BODY,{"disambiguationData":[OSD([sQuery(id+"F0.wireOp",EDGE,"E1")])]}),"instanceName":"1"}),"instanceName":"1"}),"instanceName":"1"}),"instanceName":"1"}),"instanceName":"1"}),"instanceName":"1"}),"instanceName":"1"}),"instanceName":"1"});
            var Q1055;
            Q1055=makeQuery(id+"F12.opPattern","COPY",BODY,{"derivedFrom":makeQuery(id+"F10.opPattern","COPY",BODY,{"derivedFrom":makeQuery(id+"F8.opPattern","COPY",BODY,{"derivedFrom":makeQuery(id+"F7.opPattern","COPY",BODY,{"derivedFrom":makeQuery(id+"F6.opPattern","COPY",BODY,{"derivedFrom":makeQuery(id+"F5.opPattern","COPY",BODY,{"derivedFrom":makeQuery(id+"F4.opPattern","COPY",BODY,{"derivedFrom":makeQuery(id+"F3.opPattern","COPY",BODY,{"derivedFrom":makeQuery(id+"F2.opPattern","COPY",BODY,{"derivedFrom":makeQuery(id+"F1.opRevolve","SWEPT_BODY",BODY,{"disambiguationData":[OSD([sQuery(id+"F0.wireOp",EDGE,"E1")])]}),"instanceName":"1"}),"instanceName":"1"}),"instanceName":"1"}),"instanceName":"1"}),"instanceName":"1"}),"instanceName":"1"}),"instanceName":"1"}),"instanceName":"1"}),"instanceName":"1"});
            var Q1056;
            Q1056=makeQuery(id+"F12.opPattern","COPY",BODY,{"derivedFrom":makeQuery(id+"F10.opPattern","COPY",BODY,{"derivedFrom":makeQuery(id+"F9.opPattern","COPY",BODY,{"derivedFrom":makeQuery(id+"F1.opRevolve","SWEPT_BODY",BODY,{"disambiguationData":[OSD([sQuery(id+"F0.wireOp",EDGE,"E1")])]}),"instanceName":"1"}),"instanceName":"1"}),"instanceName":"1"});
            var Q1057;
            Q1057=makeQuery(id+"F12.opPattern","COPY",BODY,{"derivedFrom":makeQuery(id+"F10.opPattern","COPY",BODY,{"derivedFrom":makeQuery(id+"F9.opPattern","COPY",BODY,{"derivedFrom":makeQuery(id+"F2.opPattern","COPY",BODY,{"derivedFrom":makeQuery(id+"F1.opRevolve","SWEPT_BODY",BODY,{"disambiguationData":[OSD([sQuery(id+"F0.wireOp",EDGE,"E1")])]}),"instanceName":"1"}),"instanceName":"1"}),"instanceName":"1"}),"instanceName":"1"});
            var Q1058;
            Q1058=makeQuery(id+"F12.opPattern","COPY",BODY,{"derivedFrom":makeQuery(id+"F10.opPattern","COPY",BODY,{"derivedFrom":makeQuery(id+"F9.opPattern","COPY",BODY,{"derivedFrom":makeQuery(id+"F3.opPattern","COPY",BODY,{"derivedFrom":makeQuery(id+"F2.opPattern","COPY",BODY,{"derivedFrom":makeQuery(id+"F1.opRevolve","SWEPT_BODY",BODY,{"disambiguationData":[OSD([sQuery(id+"F0.wireOp",EDGE,"E1")])]}),"instanceName":"1"}),"instanceName":"1"}),"instanceName":"1"}),"instanceName":"1"}),"instanceName":"1"});
            var Q1059;
            Q1059=makeQuery(id+"F12.opPattern","COPY",BODY,{"derivedFrom":makeQuery(id+"F10.opPattern","COPY",BODY,{"derivedFrom":makeQuery(id+"F9.opPattern","COPY",BODY,{"derivedFrom":makeQuery(id+"F4.opPattern","COPY",BODY,{"derivedFrom":makeQuery(id+"F1.opRevolve","SWEPT_BODY",BODY,{"disambiguationData":[OSD([sQuery(id+"F0.wireOp",EDGE,"E1")])]}),"instanceName":"1"}),"instanceName":"1"}),"instanceName":"1"}),"instanceName":"1"});
            var Q1060;
            Q1060=makeQuery(id+"F12.opPattern","COPY",BODY,{"derivedFrom":makeQuery(id+"F10.opPattern","COPY",BODY,{"derivedFrom":makeQuery(id+"F9.opPattern","COPY",BODY,{"derivedFrom":makeQuery(id+"F4.opPattern","COPY",BODY,{"derivedFrom":makeQuery(id+"F2.opPattern","COPY",BODY,{"derivedFrom":makeQuery(id+"F1.opRevolve","SWEPT_BODY",BODY,{"disambiguationData":[OSD([sQuery(id+"F0.wireOp",EDGE,"E1")])]}),"instanceName":"1"}),"instanceName":"1"}),"instanceName":"1"}),"instanceName":"1"}),"instanceName":"1"});
            var Q1061;
            Q1061=makeQuery(id+"F12.opPattern","COPY",BODY,{"derivedFrom":makeQuery(id+"F10.opPattern","COPY",BODY,{"derivedFrom":makeQuery(id+"F9.opPattern","COPY",BODY,{"derivedFrom":makeQuery(id+"F4.opPattern","COPY",BODY,{"derivedFrom":makeQuery(id+"F3.opPattern","COPY",BODY,{"derivedFrom":makeQuery(id+"F2.opPattern","COPY",BODY,{"derivedFrom":makeQuery(id+"F1.opRevolve","SWEPT_BODY",BODY,{"disambiguationData":[OSD([sQuery(id+"F0.wireOp",EDGE,"E1")])]}),"instanceName":"1"}),"instanceName":"1"}),"instanceName":"1"}),"instanceName":"1"}),"instanceName":"1"}),"instanceName":"1"});
            var Q1062;
            Q1062=makeQuery(id+"F12.opPattern","COPY",BODY,{"derivedFrom":makeQuery(id+"F10.opPattern","COPY",BODY,{"derivedFrom":makeQuery(id+"F9.opPattern","COPY",BODY,{"derivedFrom":makeQuery(id+"F5.opPattern","COPY",BODY,{"derivedFrom":makeQuery(id+"F1.opRevolve","SWEPT_BODY",BODY,{"disambiguationData":[OSD([sQuery(id+"F0.wireOp",EDGE,"E1")])]}),"instanceName":"1"}),"instanceName":"1"}),"instanceName":"1"}),"instanceName":"1"});
            var Q1063;
            Q1063=makeQuery(id+"F12.opPattern","COPY",BODY,{"derivedFrom":makeQuery(id+"F10.opPattern","COPY",BODY,{"derivedFrom":makeQuery(id+"F9.opPattern","COPY",BODY,{"derivedFrom":makeQuery(id+"F5.opPattern","COPY",BODY,{"derivedFrom":makeQuery(id+"F2.opPattern","COPY",BODY,{"derivedFrom":makeQuery(id+"F1.opRevolve","SWEPT_BODY",BODY,{"disambiguationData":[OSD([sQuery(id+"F0.wireOp",EDGE,"E1")])]}),"instanceName":"1"}),"instanceName":"1"}),"instanceName":"1"}),"instanceName":"1"}),"instanceName":"1"});
            var Q1064;
            Q1064=makeQuery(id+"F12.opPattern","COPY",BODY,{"derivedFrom":makeQuery(id+"F10.opPattern","COPY",BODY,{"derivedFrom":makeQuery(id+"F9.opPattern","COPY",BODY,{"derivedFrom":makeQuery(id+"F5.opPattern","COPY",BODY,{"derivedFrom":makeQuery(id+"F3.opPattern","COPY",BODY,{"derivedFrom":makeQuery(id+"F2.opPattern","COPY",BODY,{"derivedFrom":makeQuery(id+"F1.opRevolve","SWEPT_BODY",BODY,{"disambiguationData":[OSD([sQuery(id+"F0.wireOp",EDGE,"E1")])]}),"instanceName":"1"}),"instanceName":"1"}),"instanceName":"1"}),"instanceName":"1"}),"instanceName":"1"}),"instanceName":"1"});
            var Q1065;
            Q1065=makeQuery(id+"F12.opPattern","COPY",BODY,{"derivedFrom":makeQuery(id+"F10.opPattern","COPY",BODY,{"derivedFrom":makeQuery(id+"F9.opPattern","COPY",BODY,{"derivedFrom":makeQuery(id+"F5.opPattern","COPY",BODY,{"derivedFrom":makeQuery(id+"F4.opPattern","COPY",BODY,{"derivedFrom":makeQuery(id+"F1.opRevolve","SWEPT_BODY",BODY,{"disambiguationData":[OSD([sQuery(id+"F0.wireOp",EDGE,"E1")])]}),"instanceName":"1"}),"instanceName":"1"}),"instanceName":"1"}),"instanceName":"1"}),"instanceName":"1"});
            var Q1066;
            Q1066=makeQuery(id+"F12.opPattern","COPY",BODY,{"derivedFrom":makeQuery(id+"F10.opPattern","COPY",BODY,{"derivedFrom":makeQuery(id+"F9.opPattern","COPY",BODY,{"derivedFrom":makeQuery(id+"F5.opPattern","COPY",BODY,{"derivedFrom":makeQuery(id+"F4.opPattern","COPY",BODY,{"derivedFrom":makeQuery(id+"F2.opPattern","COPY",BODY,{"derivedFrom":makeQuery(id+"F1.opRevolve","SWEPT_BODY",BODY,{"disambiguationData":[OSD([sQuery(id+"F0.wireOp",EDGE,"E1")])]}),"instanceName":"1"}),"instanceName":"1"}),"instanceName":"1"}),"instanceName":"1"}),"instanceName":"1"}),"instanceName":"1"});
            var Q1067;
            Q1067=makeQuery(id+"F12.opPattern","COPY",BODY,{"derivedFrom":makeQuery(id+"F10.opPattern","COPY",BODY,{"derivedFrom":makeQuery(id+"F9.opPattern","COPY",BODY,{"derivedFrom":makeQuery(id+"F5.opPattern","COPY",BODY,{"derivedFrom":makeQuery(id+"F4.opPattern","COPY",BODY,{"derivedFrom":makeQuery(id+"F3.opPattern","COPY",BODY,{"derivedFrom":makeQuery(id+"F2.opPattern","COPY",BODY,{"derivedFrom":makeQuery(id+"F1.opRevolve","SWEPT_BODY",BODY,{"disambiguationData":[OSD([sQuery(id+"F0.wireOp",EDGE,"E1")])]}),"instanceName":"1"}),"instanceName":"1"}),"instanceName":"1"}),"instanceName":"1"}),"instanceName":"1"}),"instanceName":"1"}),"instanceName":"1"});
            var Q1068;
            Q1068=makeQuery(id+"F12.opPattern","COPY",BODY,{"derivedFrom":makeQuery(id+"F10.opPattern","COPY",BODY,{"derivedFrom":makeQuery(id+"F9.opPattern","COPY",BODY,{"derivedFrom":makeQuery(id+"F6.opPattern","COPY",BODY,{"derivedFrom":makeQuery(id+"F1.opRevolve","SWEPT_BODY",BODY,{"disambiguationData":[OSD([sQuery(id+"F0.wireOp",EDGE,"E1")])]}),"instanceName":"1"}),"instanceName":"1"}),"instanceName":"1"}),"instanceName":"1"});
            var Q1069;
            Q1069=makeQuery(id+"F12.opPattern","COPY",BODY,{"derivedFrom":makeQuery(id+"F10.opPattern","COPY",BODY,{"derivedFrom":makeQuery(id+"F9.opPattern","COPY",BODY,{"derivedFrom":makeQuery(id+"F6.opPattern","COPY",BODY,{"derivedFrom":makeQuery(id+"F2.opPattern","COPY",BODY,{"derivedFrom":makeQuery(id+"F1.opRevolve","SWEPT_BODY",BODY,{"disambiguationData":[OSD([sQuery(id+"F0.wireOp",EDGE,"E1")])]}),"instanceName":"1"}),"instanceName":"1"}),"instanceName":"1"}),"instanceName":"1"}),"instanceName":"1"});
            var Q1070;
            Q1070=makeQuery(id+"F12.opPattern","COPY",BODY,{"derivedFrom":makeQuery(id+"F10.opPattern","COPY",BODY,{"derivedFrom":makeQuery(id+"F9.opPattern","COPY",BODY,{"derivedFrom":makeQuery(id+"F6.opPattern","COPY",BODY,{"derivedFrom":makeQuery(id+"F3.opPattern","COPY",BODY,{"derivedFrom":makeQuery(id+"F2.opPattern","COPY",BODY,{"derivedFrom":makeQuery(id+"F1.opRevolve","SWEPT_BODY",BODY,{"disambiguationData":[OSD([sQuery(id+"F0.wireOp",EDGE,"E1")])]}),"instanceName":"1"}),"instanceName":"1"}),"instanceName":"1"}),"instanceName":"1"}),"instanceName":"1"}),"instanceName":"1"});
            var Q1071;
            Q1071=makeQuery(id+"F12.opPattern","COPY",BODY,{"derivedFrom":makeQuery(id+"F10.opPattern","COPY",BODY,{"derivedFrom":makeQuery(id+"F9.opPattern","COPY",BODY,{"derivedFrom":makeQuery(id+"F6.opPattern","COPY",BODY,{"derivedFrom":makeQuery(id+"F4.opPattern","COPY",BODY,{"derivedFrom":makeQuery(id+"F1.opRevolve","SWEPT_BODY",BODY,{"disambiguationData":[OSD([sQuery(id+"F0.wireOp",EDGE,"E1")])]}),"instanceName":"1"}),"instanceName":"1"}),"instanceName":"1"}),"instanceName":"1"}),"instanceName":"1"});
            var Q1072;
            Q1072=makeQuery(id+"F12.opPattern","COPY",BODY,{"derivedFrom":makeQuery(id+"F10.opPattern","COPY",BODY,{"derivedFrom":makeQuery(id+"F9.opPattern","COPY",BODY,{"derivedFrom":makeQuery(id+"F6.opPattern","COPY",BODY,{"derivedFrom":makeQuery(id+"F4.opPattern","COPY",BODY,{"derivedFrom":makeQuery(id+"F2.opPattern","COPY",BODY,{"derivedFrom":makeQuery(id+"F1.opRevolve","SWEPT_BODY",BODY,{"disambiguationData":[OSD([sQuery(id+"F0.wireOp",EDGE,"E1")])]}),"instanceName":"1"}),"instanceName":"1"}),"instanceName":"1"}),"instanceName":"1"}),"instanceName":"1"}),"instanceName":"1"});
            var Q1073;
            Q1073=makeQuery(id+"F12.opPattern","COPY",BODY,{"derivedFrom":makeQuery(id+"F10.opPattern","COPY",BODY,{"derivedFrom":makeQuery(id+"F9.opPattern","COPY",BODY,{"derivedFrom":makeQuery(id+"F6.opPattern","COPY",BODY,{"derivedFrom":makeQuery(id+"F4.opPattern","COPY",BODY,{"derivedFrom":makeQuery(id+"F3.opPattern","COPY",BODY,{"derivedFrom":makeQuery(id+"F2.opPattern","COPY",BODY,{"derivedFrom":makeQuery(id+"F1.opRevolve","SWEPT_BODY",BODY,{"disambiguationData":[OSD([sQuery(id+"F0.wireOp",EDGE,"E1")])]}),"instanceName":"1"}),"instanceName":"1"}),"instanceName":"1"}),"instanceName":"1"}),"instanceName":"1"}),"instanceName":"1"}),"instanceName":"1"});
            var Q1074;
            Q1074=makeQuery(id+"F12.opPattern","COPY",BODY,{"derivedFrom":makeQuery(id+"F10.opPattern","COPY",BODY,{"derivedFrom":makeQuery(id+"F9.opPattern","COPY",BODY,{"derivedFrom":makeQuery(id+"F6.opPattern","COPY",BODY,{"derivedFrom":makeQuery(id+"F5.opPattern","COPY",BODY,{"derivedFrom":makeQuery(id+"F1.opRevolve","SWEPT_BODY",BODY,{"disambiguationData":[OSD([sQuery(id+"F0.wireOp",EDGE,"E1")])]}),"instanceName":"1"}),"instanceName":"1"}),"instanceName":"1"}),"instanceName":"1"}),"instanceName":"1"});
            var Q1075;
            Q1075=makeQuery(id+"F12.opPattern","COPY",BODY,{"derivedFrom":makeQuery(id+"F10.opPattern","COPY",BODY,{"derivedFrom":makeQuery(id+"F9.opPattern","COPY",BODY,{"derivedFrom":makeQuery(id+"F6.opPattern","COPY",BODY,{"derivedFrom":makeQuery(id+"F5.opPattern","COPY",BODY,{"derivedFrom":makeQuery(id+"F2.opPattern","COPY",BODY,{"derivedFrom":makeQuery(id+"F1.opRevolve","SWEPT_BODY",BODY,{"disambiguationData":[OSD([sQuery(id+"F0.wireOp",EDGE,"E1")])]}),"instanceName":"1"}),"instanceName":"1"}),"instanceName":"1"}),"instanceName":"1"}),"instanceName":"1"}),"instanceName":"1"});
            var Q1076;
            Q1076=makeQuery(id+"F12.opPattern","COPY",BODY,{"derivedFrom":makeQuery(id+"F10.opPattern","COPY",BODY,{"derivedFrom":makeQuery(id+"F9.opPattern","COPY",BODY,{"derivedFrom":makeQuery(id+"F6.opPattern","COPY",BODY,{"derivedFrom":makeQuery(id+"F5.opPattern","COPY",BODY,{"derivedFrom":makeQuery(id+"F3.opPattern","COPY",BODY,{"derivedFrom":makeQuery(id+"F2.opPattern","COPY",BODY,{"derivedFrom":makeQuery(id+"F1.opRevolve","SWEPT_BODY",BODY,{"disambiguationData":[OSD([sQuery(id+"F0.wireOp",EDGE,"E1")])]}),"instanceName":"1"}),"instanceName":"1"}),"instanceName":"1"}),"instanceName":"1"}),"instanceName":"1"}),"instanceName":"1"}),"instanceName":"1"});
            var Q1077;
            Q1077=makeQuery(id+"F12.opPattern","COPY",BODY,{"derivedFrom":makeQuery(id+"F10.opPattern","COPY",BODY,{"derivedFrom":makeQuery(id+"F9.opPattern","COPY",BODY,{"derivedFrom":makeQuery(id+"F6.opPattern","COPY",BODY,{"derivedFrom":makeQuery(id+"F5.opPattern","COPY",BODY,{"derivedFrom":makeQuery(id+"F4.opPattern","COPY",BODY,{"derivedFrom":makeQuery(id+"F1.opRevolve","SWEPT_BODY",BODY,{"disambiguationData":[OSD([sQuery(id+"F0.wireOp",EDGE,"E1")])]}),"instanceName":"1"}),"instanceName":"1"}),"instanceName":"1"}),"instanceName":"1"}),"instanceName":"1"}),"instanceName":"1"});
            var Q1078;
            Q1078=makeQuery(id+"F12.opPattern","COPY",BODY,{"derivedFrom":makeQuery(id+"F10.opPattern","COPY",BODY,{"derivedFrom":makeQuery(id+"F9.opPattern","COPY",BODY,{"derivedFrom":makeQuery(id+"F6.opPattern","COPY",BODY,{"derivedFrom":makeQuery(id+"F5.opPattern","COPY",BODY,{"derivedFrom":makeQuery(id+"F4.opPattern","COPY",BODY,{"derivedFrom":makeQuery(id+"F2.opPattern","COPY",BODY,{"derivedFrom":makeQuery(id+"F1.opRevolve","SWEPT_BODY",BODY,{"disambiguationData":[OSD([sQuery(id+"F0.wireOp",EDGE,"E1")])]}),"instanceName":"1"}),"instanceName":"1"}),"instanceName":"1"}),"instanceName":"1"}),"instanceName":"1"}),"instanceName":"1"}),"instanceName":"1"});
            var Q1079;
            Q1079=makeQuery(id+"F12.opPattern","COPY",BODY,{"derivedFrom":makeQuery(id+"F10.opPattern","COPY",BODY,{"derivedFrom":makeQuery(id+"F9.opPattern","COPY",BODY,{"derivedFrom":makeQuery(id+"F6.opPattern","COPY",BODY,{"derivedFrom":makeQuery(id+"F5.opPattern","COPY",BODY,{"derivedFrom":makeQuery(id+"F4.opPattern","COPY",BODY,{"derivedFrom":makeQuery(id+"F3.opPattern","COPY",BODY,{"derivedFrom":makeQuery(id+"F2.opPattern","COPY",BODY,{"derivedFrom":makeQuery(id+"F1.opRevolve","SWEPT_BODY",BODY,{"disambiguationData":[OSD([sQuery(id+"F0.wireOp",EDGE,"E1")])]}),"instanceName":"1"}),"instanceName":"1"}),"instanceName":"1"}),"instanceName":"1"}),"instanceName":"1"}),"instanceName":"1"}),"instanceName":"1"}),"instanceName":"1"});
            var Q1080;
            Q1080=makeQuery(id+"F12.opPattern","COPY",BODY,{"derivedFrom":makeQuery(id+"F10.opPattern","COPY",BODY,{"derivedFrom":makeQuery(id+"F9.opPattern","COPY",BODY,{"derivedFrom":makeQuery(id+"F7.opPattern","COPY",BODY,{"derivedFrom":makeQuery(id+"F1.opRevolve","SWEPT_BODY",BODY,{"disambiguationData":[OSD([sQuery(id+"F0.wireOp",EDGE,"E1")])]}),"instanceName":"1"}),"instanceName":"1"}),"instanceName":"1"}),"instanceName":"1"});
            var Q1081;
            Q1081=makeQuery(id+"F12.opPattern","COPY",BODY,{"derivedFrom":makeQuery(id+"F10.opPattern","COPY",BODY,{"derivedFrom":makeQuery(id+"F9.opPattern","COPY",BODY,{"derivedFrom":makeQuery(id+"F7.opPattern","COPY",BODY,{"derivedFrom":makeQuery(id+"F2.opPattern","COPY",BODY,{"derivedFrom":makeQuery(id+"F1.opRevolve","SWEPT_BODY",BODY,{"disambiguationData":[OSD([sQuery(id+"F0.wireOp",EDGE,"E1")])]}),"instanceName":"1"}),"instanceName":"1"}),"instanceName":"1"}),"instanceName":"1"}),"instanceName":"1"});
            var Q1082;
            Q1082=makeQuery(id+"F12.opPattern","COPY",BODY,{"derivedFrom":makeQuery(id+"F10.opPattern","COPY",BODY,{"derivedFrom":makeQuery(id+"F9.opPattern","COPY",BODY,{"derivedFrom":makeQuery(id+"F7.opPattern","COPY",BODY,{"derivedFrom":makeQuery(id+"F3.opPattern","COPY",BODY,{"derivedFrom":makeQuery(id+"F2.opPattern","COPY",BODY,{"derivedFrom":makeQuery(id+"F1.opRevolve","SWEPT_BODY",BODY,{"disambiguationData":[OSD([sQuery(id+"F0.wireOp",EDGE,"E1")])]}),"instanceName":"1"}),"instanceName":"1"}),"instanceName":"1"}),"instanceName":"1"}),"instanceName":"1"}),"instanceName":"1"});
            var Q1083;
            Q1083=makeQuery(id+"F12.opPattern","COPY",BODY,{"derivedFrom":makeQuery(id+"F10.opPattern","COPY",BODY,{"derivedFrom":makeQuery(id+"F9.opPattern","COPY",BODY,{"derivedFrom":makeQuery(id+"F7.opPattern","COPY",BODY,{"derivedFrom":makeQuery(id+"F4.opPattern","COPY",BODY,{"derivedFrom":makeQuery(id+"F1.opRevolve","SWEPT_BODY",BODY,{"disambiguationData":[OSD([sQuery(id+"F0.wireOp",EDGE,"E1")])]}),"instanceName":"1"}),"instanceName":"1"}),"instanceName":"1"}),"instanceName":"1"}),"instanceName":"1"});
            var Q1084;
            Q1084=makeQuery(id+"F12.opPattern","COPY",BODY,{"derivedFrom":makeQuery(id+"F10.opPattern","COPY",BODY,{"derivedFrom":makeQuery(id+"F9.opPattern","COPY",BODY,{"derivedFrom":makeQuery(id+"F7.opPattern","COPY",BODY,{"derivedFrom":makeQuery(id+"F4.opPattern","COPY",BODY,{"derivedFrom":makeQuery(id+"F2.opPattern","COPY",BODY,{"derivedFrom":makeQuery(id+"F1.opRevolve","SWEPT_BODY",BODY,{"disambiguationData":[OSD([sQuery(id+"F0.wireOp",EDGE,"E1")])]}),"instanceName":"1"}),"instanceName":"1"}),"instanceName":"1"}),"instanceName":"1"}),"instanceName":"1"}),"instanceName":"1"});
            var Q1085;
            Q1085=makeQuery(id+"F12.opPattern","COPY",BODY,{"derivedFrom":makeQuery(id+"F10.opPattern","COPY",BODY,{"derivedFrom":makeQuery(id+"F9.opPattern","COPY",BODY,{"derivedFrom":makeQuery(id+"F7.opPattern","COPY",BODY,{"derivedFrom":makeQuery(id+"F4.opPattern","COPY",BODY,{"derivedFrom":makeQuery(id+"F3.opPattern","COPY",BODY,{"derivedFrom":makeQuery(id+"F2.opPattern","COPY",BODY,{"derivedFrom":makeQuery(id+"F1.opRevolve","SWEPT_BODY",BODY,{"disambiguationData":[OSD([sQuery(id+"F0.wireOp",EDGE,"E1")])]}),"instanceName":"1"}),"instanceName":"1"}),"instanceName":"1"}),"instanceName":"1"}),"instanceName":"1"}),"instanceName":"1"}),"instanceName":"1"});
            var Q1086;
            Q1086=makeQuery(id+"F12.opPattern","COPY",BODY,{"derivedFrom":makeQuery(id+"F10.opPattern","COPY",BODY,{"derivedFrom":makeQuery(id+"F9.opPattern","COPY",BODY,{"derivedFrom":makeQuery(id+"F7.opPattern","COPY",BODY,{"derivedFrom":makeQuery(id+"F5.opPattern","COPY",BODY,{"derivedFrom":makeQuery(id+"F1.opRevolve","SWEPT_BODY",BODY,{"disambiguationData":[OSD([sQuery(id+"F0.wireOp",EDGE,"E1")])]}),"instanceName":"1"}),"instanceName":"1"}),"instanceName":"1"}),"instanceName":"1"}),"instanceName":"1"});
            var Q1087;
            Q1087=makeQuery(id+"F12.opPattern","COPY",BODY,{"derivedFrom":makeQuery(id+"F10.opPattern","COPY",BODY,{"derivedFrom":makeQuery(id+"F9.opPattern","COPY",BODY,{"derivedFrom":makeQuery(id+"F7.opPattern","COPY",BODY,{"derivedFrom":makeQuery(id+"F5.opPattern","COPY",BODY,{"derivedFrom":makeQuery(id+"F2.opPattern","COPY",BODY,{"derivedFrom":makeQuery(id+"F1.opRevolve","SWEPT_BODY",BODY,{"disambiguationData":[OSD([sQuery(id+"F0.wireOp",EDGE,"E1")])]}),"instanceName":"1"}),"instanceName":"1"}),"instanceName":"1"}),"instanceName":"1"}),"instanceName":"1"}),"instanceName":"1"});
            var Q1088;
            Q1088=makeQuery(id+"F12.opPattern","COPY",BODY,{"derivedFrom":makeQuery(id+"F10.opPattern","COPY",BODY,{"derivedFrom":makeQuery(id+"F9.opPattern","COPY",BODY,{"derivedFrom":makeQuery(id+"F7.opPattern","COPY",BODY,{"derivedFrom":makeQuery(id+"F5.opPattern","COPY",BODY,{"derivedFrom":makeQuery(id+"F3.opPattern","COPY",BODY,{"derivedFrom":makeQuery(id+"F2.opPattern","COPY",BODY,{"derivedFrom":makeQuery(id+"F1.opRevolve","SWEPT_BODY",BODY,{"disambiguationData":[OSD([sQuery(id+"F0.wireOp",EDGE,"E1")])]}),"instanceName":"1"}),"instanceName":"1"}),"instanceName":"1"}),"instanceName":"1"}),"instanceName":"1"}),"instanceName":"1"}),"instanceName":"1"});
            var Q1089;
            Q1089=makeQuery(id+"F12.opPattern","COPY",BODY,{"derivedFrom":makeQuery(id+"F10.opPattern","COPY",BODY,{"derivedFrom":makeQuery(id+"F9.opPattern","COPY",BODY,{"derivedFrom":makeQuery(id+"F7.opPattern","COPY",BODY,{"derivedFrom":makeQuery(id+"F5.opPattern","COPY",BODY,{"derivedFrom":makeQuery(id+"F4.opPattern","COPY",BODY,{"derivedFrom":makeQuery(id+"F1.opRevolve","SWEPT_BODY",BODY,{"disambiguationData":[OSD([sQuery(id+"F0.wireOp",EDGE,"E1")])]}),"instanceName":"1"}),"instanceName":"1"}),"instanceName":"1"}),"instanceName":"1"}),"instanceName":"1"}),"instanceName":"1"});
            var Q1090;
            Q1090=makeQuery(id+"F12.opPattern","COPY",BODY,{"derivedFrom":makeQuery(id+"F10.opPattern","COPY",BODY,{"derivedFrom":makeQuery(id+"F9.opPattern","COPY",BODY,{"derivedFrom":makeQuery(id+"F7.opPattern","COPY",BODY,{"derivedFrom":makeQuery(id+"F5.opPattern","COPY",BODY,{"derivedFrom":makeQuery(id+"F4.opPattern","COPY",BODY,{"derivedFrom":makeQuery(id+"F2.opPattern","COPY",BODY,{"derivedFrom":makeQuery(id+"F1.opRevolve","SWEPT_BODY",BODY,{"disambiguationData":[OSD([sQuery(id+"F0.wireOp",EDGE,"E1")])]}),"instanceName":"1"}),"instanceName":"1"}),"instanceName":"1"}),"instanceName":"1"}),"instanceName":"1"}),"instanceName":"1"}),"instanceName":"1"});
            var Q1091;
            Q1091=makeQuery(id+"F12.opPattern","COPY",BODY,{"derivedFrom":makeQuery(id+"F10.opPattern","COPY",BODY,{"derivedFrom":makeQuery(id+"F9.opPattern","COPY",BODY,{"derivedFrom":makeQuery(id+"F7.opPattern","COPY",BODY,{"derivedFrom":makeQuery(id+"F5.opPattern","COPY",BODY,{"derivedFrom":makeQuery(id+"F4.opPattern","COPY",BODY,{"derivedFrom":makeQuery(id+"F3.opPattern","COPY",BODY,{"derivedFrom":makeQuery(id+"F2.opPattern","COPY",BODY,{"derivedFrom":makeQuery(id+"F1.opRevolve","SWEPT_BODY",BODY,{"disambiguationData":[OSD([sQuery(id+"F0.wireOp",EDGE,"E1")])]}),"instanceName":"1"}),"instanceName":"1"}),"instanceName":"1"}),"instanceName":"1"}),"instanceName":"1"}),"instanceName":"1"}),"instanceName":"1"}),"instanceName":"1"});
            var Q1092;
            Q1092=makeQuery(id+"F12.opPattern","COPY",BODY,{"derivedFrom":makeQuery(id+"F10.opPattern","COPY",BODY,{"derivedFrom":makeQuery(id+"F9.opPattern","COPY",BODY,{"derivedFrom":makeQuery(id+"F7.opPattern","COPY",BODY,{"derivedFrom":makeQuery(id+"F6.opPattern","COPY",BODY,{"derivedFrom":makeQuery(id+"F1.opRevolve","SWEPT_BODY",BODY,{"disambiguationData":[OSD([sQuery(id+"F0.wireOp",EDGE,"E1")])]}),"instanceName":"1"}),"instanceName":"1"}),"instanceName":"1"}),"instanceName":"1"}),"instanceName":"1"});
            var Q1093;
            Q1093=makeQuery(id+"F12.opPattern","COPY",BODY,{"derivedFrom":makeQuery(id+"F10.opPattern","COPY",BODY,{"derivedFrom":makeQuery(id+"F9.opPattern","COPY",BODY,{"derivedFrom":makeQuery(id+"F7.opPattern","COPY",BODY,{"derivedFrom":makeQuery(id+"F6.opPattern","COPY",BODY,{"derivedFrom":makeQuery(id+"F2.opPattern","COPY",BODY,{"derivedFrom":makeQuery(id+"F1.opRevolve","SWEPT_BODY",BODY,{"disambiguationData":[OSD([sQuery(id+"F0.wireOp",EDGE,"E1")])]}),"instanceName":"1"}),"instanceName":"1"}),"instanceName":"1"}),"instanceName":"1"}),"instanceName":"1"}),"instanceName":"1"});
            var Q1094;
            Q1094=makeQuery(id+"F12.opPattern","COPY",BODY,{"derivedFrom":makeQuery(id+"F10.opPattern","COPY",BODY,{"derivedFrom":makeQuery(id+"F9.opPattern","COPY",BODY,{"derivedFrom":makeQuery(id+"F7.opPattern","COPY",BODY,{"derivedFrom":makeQuery(id+"F6.opPattern","COPY",BODY,{"derivedFrom":makeQuery(id+"F3.opPattern","COPY",BODY,{"derivedFrom":makeQuery(id+"F2.opPattern","COPY",BODY,{"derivedFrom":makeQuery(id+"F1.opRevolve","SWEPT_BODY",BODY,{"disambiguationData":[OSD([sQuery(id+"F0.wireOp",EDGE,"E1")])]}),"instanceName":"1"}),"instanceName":"1"}),"instanceName":"1"}),"instanceName":"1"}),"instanceName":"1"}),"instanceName":"1"}),"instanceName":"1"});
            var Q1095;
            Q1095=makeQuery(id+"F12.opPattern","COPY",BODY,{"derivedFrom":makeQuery(id+"F10.opPattern","COPY",BODY,{"derivedFrom":makeQuery(id+"F9.opPattern","COPY",BODY,{"derivedFrom":makeQuery(id+"F7.opPattern","COPY",BODY,{"derivedFrom":makeQuery(id+"F6.opPattern","COPY",BODY,{"derivedFrom":makeQuery(id+"F4.opPattern","COPY",BODY,{"derivedFrom":makeQuery(id+"F1.opRevolve","SWEPT_BODY",BODY,{"disambiguationData":[OSD([sQuery(id+"F0.wireOp",EDGE,"E1")])]}),"instanceName":"1"}),"instanceName":"1"}),"instanceName":"1"}),"instanceName":"1"}),"instanceName":"1"}),"instanceName":"1"});
            var Q1096;
            Q1096=makeQuery(id+"F12.opPattern","COPY",BODY,{"derivedFrom":makeQuery(id+"F10.opPattern","COPY",BODY,{"derivedFrom":makeQuery(id+"F9.opPattern","COPY",BODY,{"derivedFrom":makeQuery(id+"F7.opPattern","COPY",BODY,{"derivedFrom":makeQuery(id+"F6.opPattern","COPY",BODY,{"derivedFrom":makeQuery(id+"F4.opPattern","COPY",BODY,{"derivedFrom":makeQuery(id+"F2.opPattern","COPY",BODY,{"derivedFrom":makeQuery(id+"F1.opRevolve","SWEPT_BODY",BODY,{"disambiguationData":[OSD([sQuery(id+"F0.wireOp",EDGE,"E1")])]}),"instanceName":"1"}),"instanceName":"1"}),"instanceName":"1"}),"instanceName":"1"}),"instanceName":"1"}),"instanceName":"1"}),"instanceName":"1"});
            var Q1097;
            Q1097=makeQuery(id+"F12.opPattern","COPY",BODY,{"derivedFrom":makeQuery(id+"F10.opPattern","COPY",BODY,{"derivedFrom":makeQuery(id+"F9.opPattern","COPY",BODY,{"derivedFrom":makeQuery(id+"F7.opPattern","COPY",BODY,{"derivedFrom":makeQuery(id+"F6.opPattern","COPY",BODY,{"derivedFrom":makeQuery(id+"F4.opPattern","COPY",BODY,{"derivedFrom":makeQuery(id+"F3.opPattern","COPY",BODY,{"derivedFrom":makeQuery(id+"F2.opPattern","COPY",BODY,{"derivedFrom":makeQuery(id+"F1.opRevolve","SWEPT_BODY",BODY,{"disambiguationData":[OSD([sQuery(id+"F0.wireOp",EDGE,"E1")])]}),"instanceName":"1"}),"instanceName":"1"}),"instanceName":"1"}),"instanceName":"1"}),"instanceName":"1"}),"instanceName":"1"}),"instanceName":"1"}),"instanceName":"1"});
            var Q1098;
            Q1098=makeQuery(id+"F12.opPattern","COPY",BODY,{"derivedFrom":makeQuery(id+"F10.opPattern","COPY",BODY,{"derivedFrom":makeQuery(id+"F9.opPattern","COPY",BODY,{"derivedFrom":makeQuery(id+"F7.opPattern","COPY",BODY,{"derivedFrom":makeQuery(id+"F6.opPattern","COPY",BODY,{"derivedFrom":makeQuery(id+"F5.opPattern","COPY",BODY,{"derivedFrom":makeQuery(id+"F1.opRevolve","SWEPT_BODY",BODY,{"disambiguationData":[OSD([sQuery(id+"F0.wireOp",EDGE,"E1")])]}),"instanceName":"1"}),"instanceName":"1"}),"instanceName":"1"}),"instanceName":"1"}),"instanceName":"1"}),"instanceName":"1"});
            var Q1099;
            Q1099=makeQuery(id+"F12.opPattern","COPY",BODY,{"derivedFrom":makeQuery(id+"F10.opPattern","COPY",BODY,{"derivedFrom":makeQuery(id+"F9.opPattern","COPY",BODY,{"derivedFrom":makeQuery(id+"F7.opPattern","COPY",BODY,{"derivedFrom":makeQuery(id+"F6.opPattern","COPY",BODY,{"derivedFrom":makeQuery(id+"F5.opPattern","COPY",BODY,{"derivedFrom":makeQuery(id+"F2.opPattern","COPY",BODY,{"derivedFrom":makeQuery(id+"F1.opRevolve","SWEPT_BODY",BODY,{"disambiguationData":[OSD([sQuery(id+"F0.wireOp",EDGE,"E1")])]}),"instanceName":"1"}),"instanceName":"1"}),"instanceName":"1"}),"instanceName":"1"}),"instanceName":"1"}),"instanceName":"1"}),"instanceName":"1"});
            var Q1100;
            Q1100=makeQuery(id+"F12.opPattern","COPY",BODY,{"derivedFrom":makeQuery(id+"F10.opPattern","COPY",BODY,{"derivedFrom":makeQuery(id+"F9.opPattern","COPY",BODY,{"derivedFrom":makeQuery(id+"F7.opPattern","COPY",BODY,{"derivedFrom":makeQuery(id+"F6.opPattern","COPY",BODY,{"derivedFrom":makeQuery(id+"F5.opPattern","COPY",BODY,{"derivedFrom":makeQuery(id+"F3.opPattern","COPY",BODY,{"derivedFrom":makeQuery(id+"F2.opPattern","COPY",BODY,{"derivedFrom":makeQuery(id+"F1.opRevolve","SWEPT_BODY",BODY,{"disambiguationData":[OSD([sQuery(id+"F0.wireOp",EDGE,"E1")])]}),"instanceName":"1"}),"instanceName":"1"}),"instanceName":"1"}),"instanceName":"1"}),"instanceName":"1"}),"instanceName":"1"}),"instanceName":"1"}),"instanceName":"1"});
            var Q1101;
            Q1101=makeQuery(id+"F12.opPattern","COPY",BODY,{"derivedFrom":makeQuery(id+"F10.opPattern","COPY",BODY,{"derivedFrom":makeQuery(id+"F9.opPattern","COPY",BODY,{"derivedFrom":makeQuery(id+"F7.opPattern","COPY",BODY,{"derivedFrom":makeQuery(id+"F6.opPattern","COPY",BODY,{"derivedFrom":makeQuery(id+"F5.opPattern","COPY",BODY,{"derivedFrom":makeQuery(id+"F4.opPattern","COPY",BODY,{"derivedFrom":makeQuery(id+"F1.opRevolve","SWEPT_BODY",BODY,{"disambiguationData":[OSD([sQuery(id+"F0.wireOp",EDGE,"E1")])]}),"instanceName":"1"}),"instanceName":"1"}),"instanceName":"1"}),"instanceName":"1"}),"instanceName":"1"}),"instanceName":"1"}),"instanceName":"1"});
            var Q1102;
            Q1102=makeQuery(id+"F12.opPattern","COPY",BODY,{"derivedFrom":makeQuery(id+"F10.opPattern","COPY",BODY,{"derivedFrom":makeQuery(id+"F9.opPattern","COPY",BODY,{"derivedFrom":makeQuery(id+"F7.opPattern","COPY",BODY,{"derivedFrom":makeQuery(id+"F6.opPattern","COPY",BODY,{"derivedFrom":makeQuery(id+"F5.opPattern","COPY",BODY,{"derivedFrom":makeQuery(id+"F4.opPattern","COPY",BODY,{"derivedFrom":makeQuery(id+"F2.opPattern","COPY",BODY,{"derivedFrom":makeQuery(id+"F1.opRevolve","SWEPT_BODY",BODY,{"disambiguationData":[OSD([sQuery(id+"F0.wireOp",EDGE,"E1")])]}),"instanceName":"1"}),"instanceName":"1"}),"instanceName":"1"}),"instanceName":"1"}),"instanceName":"1"}),"instanceName":"1"}),"instanceName":"1"}),"instanceName":"1"});
            var Q1103;
            Q1103=makeQuery(id+"F12.opPattern","COPY",BODY,{"derivedFrom":makeQuery(id+"F10.opPattern","COPY",BODY,{"derivedFrom":makeQuery(id+"F9.opPattern","COPY",BODY,{"derivedFrom":makeQuery(id+"F7.opPattern","COPY",BODY,{"derivedFrom":makeQuery(id+"F6.opPattern","COPY",BODY,{"derivedFrom":makeQuery(id+"F5.opPattern","COPY",BODY,{"derivedFrom":makeQuery(id+"F4.opPattern","COPY",BODY,{"derivedFrom":makeQuery(id+"F3.opPattern","COPY",BODY,{"derivedFrom":makeQuery(id+"F2.opPattern","COPY",BODY,{"derivedFrom":makeQuery(id+"F1.opRevolve","SWEPT_BODY",BODY,{"disambiguationData":[OSD([sQuery(id+"F0.wireOp",EDGE,"E1")])]}),"instanceName":"1"}),"instanceName":"1"}),"instanceName":"1"}),"instanceName":"1"}),"instanceName":"1"}),"instanceName":"1"}),"instanceName":"1"}),"instanceName":"1"}),"instanceName":"1"});
            var Q1104;
            Q1104=makeQuery(id+"F12.opPattern","COPY",BODY,{"derivedFrom":makeQuery(id+"F10.opPattern","COPY",BODY,{"derivedFrom":makeQuery(id+"F9.opPattern","COPY",BODY,{"derivedFrom":makeQuery(id+"F8.opPattern","COPY",BODY,{"derivedFrom":makeQuery(id+"F1.opRevolve","SWEPT_BODY",BODY,{"disambiguationData":[OSD([sQuery(id+"F0.wireOp",EDGE,"E1")])]}),"instanceName":"1"}),"instanceName":"1"}),"instanceName":"1"}),"instanceName":"1"});
            var Q1105;
            Q1105=makeQuery(id+"F12.opPattern","COPY",BODY,{"derivedFrom":makeQuery(id+"F10.opPattern","COPY",BODY,{"derivedFrom":makeQuery(id+"F9.opPattern","COPY",BODY,{"derivedFrom":makeQuery(id+"F8.opPattern","COPY",BODY,{"derivedFrom":makeQuery(id+"F2.opPattern","COPY",BODY,{"derivedFrom":makeQuery(id+"F1.opRevolve","SWEPT_BODY",BODY,{"disambiguationData":[OSD([sQuery(id+"F0.wireOp",EDGE,"E1")])]}),"instanceName":"1"}),"instanceName":"1"}),"instanceName":"1"}),"instanceName":"1"}),"instanceName":"1"});
            var Q1106;
            Q1106=makeQuery(id+"F12.opPattern","COPY",BODY,{"derivedFrom":makeQuery(id+"F10.opPattern","COPY",BODY,{"derivedFrom":makeQuery(id+"F9.opPattern","COPY",BODY,{"derivedFrom":makeQuery(id+"F8.opPattern","COPY",BODY,{"derivedFrom":makeQuery(id+"F3.opPattern","COPY",BODY,{"derivedFrom":makeQuery(id+"F2.opPattern","COPY",BODY,{"derivedFrom":makeQuery(id+"F1.opRevolve","SWEPT_BODY",BODY,{"disambiguationData":[OSD([sQuery(id+"F0.wireOp",EDGE,"E1")])]}),"instanceName":"1"}),"instanceName":"1"}),"instanceName":"1"}),"instanceName":"1"}),"instanceName":"1"}),"instanceName":"1"});
            var Q1107;
            Q1107=makeQuery(id+"F12.opPattern","COPY",BODY,{"derivedFrom":makeQuery(id+"F10.opPattern","COPY",BODY,{"derivedFrom":makeQuery(id+"F9.opPattern","COPY",BODY,{"derivedFrom":makeQuery(id+"F8.opPattern","COPY",BODY,{"derivedFrom":makeQuery(id+"F4.opPattern","COPY",BODY,{"derivedFrom":makeQuery(id+"F1.opRevolve","SWEPT_BODY",BODY,{"disambiguationData":[OSD([sQuery(id+"F0.wireOp",EDGE,"E1")])]}),"instanceName":"1"}),"instanceName":"1"}),"instanceName":"1"}),"instanceName":"1"}),"instanceName":"1"});
            var Q1108;
            Q1108=makeQuery(id+"F12.opPattern","COPY",BODY,{"derivedFrom":makeQuery(id+"F10.opPattern","COPY",BODY,{"derivedFrom":makeQuery(id+"F9.opPattern","COPY",BODY,{"derivedFrom":makeQuery(id+"F8.opPattern","COPY",BODY,{"derivedFrom":makeQuery(id+"F4.opPattern","COPY",BODY,{"derivedFrom":makeQuery(id+"F2.opPattern","COPY",BODY,{"derivedFrom":makeQuery(id+"F1.opRevolve","SWEPT_BODY",BODY,{"disambiguationData":[OSD([sQuery(id+"F0.wireOp",EDGE,"E1")])]}),"instanceName":"1"}),"instanceName":"1"}),"instanceName":"1"}),"instanceName":"1"}),"instanceName":"1"}),"instanceName":"1"});
            var Q1109;
            Q1109=makeQuery(id+"F12.opPattern","COPY",BODY,{"derivedFrom":makeQuery(id+"F10.opPattern","COPY",BODY,{"derivedFrom":makeQuery(id+"F9.opPattern","COPY",BODY,{"derivedFrom":makeQuery(id+"F8.opPattern","COPY",BODY,{"derivedFrom":makeQuery(id+"F4.opPattern","COPY",BODY,{"derivedFrom":makeQuery(id+"F3.opPattern","COPY",BODY,{"derivedFrom":makeQuery(id+"F2.opPattern","COPY",BODY,{"derivedFrom":makeQuery(id+"F1.opRevolve","SWEPT_BODY",BODY,{"disambiguationData":[OSD([sQuery(id+"F0.wireOp",EDGE,"E1")])]}),"instanceName":"1"}),"instanceName":"1"}),"instanceName":"1"}),"instanceName":"1"}),"instanceName":"1"}),"instanceName":"1"}),"instanceName":"1"});
            var Q1110;
            Q1110=makeQuery(id+"F12.opPattern","COPY",BODY,{"derivedFrom":makeQuery(id+"F10.opPattern","COPY",BODY,{"derivedFrom":makeQuery(id+"F9.opPattern","COPY",BODY,{"derivedFrom":makeQuery(id+"F8.opPattern","COPY",BODY,{"derivedFrom":makeQuery(id+"F5.opPattern","COPY",BODY,{"derivedFrom":makeQuery(id+"F1.opRevolve","SWEPT_BODY",BODY,{"disambiguationData":[OSD([sQuery(id+"F0.wireOp",EDGE,"E1")])]}),"instanceName":"1"}),"instanceName":"1"}),"instanceName":"1"}),"instanceName":"1"}),"instanceName":"1"});
            var Q1111;
            Q1111=makeQuery(id+"F12.opPattern","COPY",BODY,{"derivedFrom":makeQuery(id+"F10.opPattern","COPY",BODY,{"derivedFrom":makeQuery(id+"F9.opPattern","COPY",BODY,{"derivedFrom":makeQuery(id+"F8.opPattern","COPY",BODY,{"derivedFrom":makeQuery(id+"F5.opPattern","COPY",BODY,{"derivedFrom":makeQuery(id+"F2.opPattern","COPY",BODY,{"derivedFrom":makeQuery(id+"F1.opRevolve","SWEPT_BODY",BODY,{"disambiguationData":[OSD([sQuery(id+"F0.wireOp",EDGE,"E1")])]}),"instanceName":"1"}),"instanceName":"1"}),"instanceName":"1"}),"instanceName":"1"}),"instanceName":"1"}),"instanceName":"1"});
            var Q1112;
            Q1112=makeQuery(id+"F12.opPattern","COPY",BODY,{"derivedFrom":makeQuery(id+"F10.opPattern","COPY",BODY,{"derivedFrom":makeQuery(id+"F9.opPattern","COPY",BODY,{"derivedFrom":makeQuery(id+"F8.opPattern","COPY",BODY,{"derivedFrom":makeQuery(id+"F5.opPattern","COPY",BODY,{"derivedFrom":makeQuery(id+"F3.opPattern","COPY",BODY,{"derivedFrom":makeQuery(id+"F2.opPattern","COPY",BODY,{"derivedFrom":makeQuery(id+"F1.opRevolve","SWEPT_BODY",BODY,{"disambiguationData":[OSD([sQuery(id+"F0.wireOp",EDGE,"E1")])]}),"instanceName":"1"}),"instanceName":"1"}),"instanceName":"1"}),"instanceName":"1"}),"instanceName":"1"}),"instanceName":"1"}),"instanceName":"1"});
            var Q1113;
            Q1113=makeQuery(id+"F12.opPattern","COPY",BODY,{"derivedFrom":makeQuery(id+"F10.opPattern","COPY",BODY,{"derivedFrom":makeQuery(id+"F9.opPattern","COPY",BODY,{"derivedFrom":makeQuery(id+"F8.opPattern","COPY",BODY,{"derivedFrom":makeQuery(id+"F5.opPattern","COPY",BODY,{"derivedFrom":makeQuery(id+"F4.opPattern","COPY",BODY,{"derivedFrom":makeQuery(id+"F1.opRevolve","SWEPT_BODY",BODY,{"disambiguationData":[OSD([sQuery(id+"F0.wireOp",EDGE,"E1")])]}),"instanceName":"1"}),"instanceName":"1"}),"instanceName":"1"}),"instanceName":"1"}),"instanceName":"1"}),"instanceName":"1"});
            var Q1114;
            Q1114=makeQuery(id+"F12.opPattern","COPY",BODY,{"derivedFrom":makeQuery(id+"F10.opPattern","COPY",BODY,{"derivedFrom":makeQuery(id+"F9.opPattern","COPY",BODY,{"derivedFrom":makeQuery(id+"F8.opPattern","COPY",BODY,{"derivedFrom":makeQuery(id+"F5.opPattern","COPY",BODY,{"derivedFrom":makeQuery(id+"F4.opPattern","COPY",BODY,{"derivedFrom":makeQuery(id+"F2.opPattern","COPY",BODY,{"derivedFrom":makeQuery(id+"F1.opRevolve","SWEPT_BODY",BODY,{"disambiguationData":[OSD([sQuery(id+"F0.wireOp",EDGE,"E1")])]}),"instanceName":"1"}),"instanceName":"1"}),"instanceName":"1"}),"instanceName":"1"}),"instanceName":"1"}),"instanceName":"1"}),"instanceName":"1"});
            var Q1115;
            Q1115=makeQuery(id+"F12.opPattern","COPY",BODY,{"derivedFrom":makeQuery(id+"F10.opPattern","COPY",BODY,{"derivedFrom":makeQuery(id+"F9.opPattern","COPY",BODY,{"derivedFrom":makeQuery(id+"F8.opPattern","COPY",BODY,{"derivedFrom":makeQuery(id+"F5.opPattern","COPY",BODY,{"derivedFrom":makeQuery(id+"F4.opPattern","COPY",BODY,{"derivedFrom":makeQuery(id+"F3.opPattern","COPY",BODY,{"derivedFrom":makeQuery(id+"F2.opPattern","COPY",BODY,{"derivedFrom":makeQuery(id+"F1.opRevolve","SWEPT_BODY",BODY,{"disambiguationData":[OSD([sQuery(id+"F0.wireOp",EDGE,"E1")])]}),"instanceName":"1"}),"instanceName":"1"}),"instanceName":"1"}),"instanceName":"1"}),"instanceName":"1"}),"instanceName":"1"}),"instanceName":"1"}),"instanceName":"1"});
            var Q1116;
            Q1116=makeQuery(id+"F12.opPattern","COPY",BODY,{"derivedFrom":makeQuery(id+"F10.opPattern","COPY",BODY,{"derivedFrom":makeQuery(id+"F9.opPattern","COPY",BODY,{"derivedFrom":makeQuery(id+"F8.opPattern","COPY",BODY,{"derivedFrom":makeQuery(id+"F6.opPattern","COPY",BODY,{"derivedFrom":makeQuery(id+"F1.opRevolve","SWEPT_BODY",BODY,{"disambiguationData":[OSD([sQuery(id+"F0.wireOp",EDGE,"E1")])]}),"instanceName":"1"}),"instanceName":"1"}),"instanceName":"1"}),"instanceName":"1"}),"instanceName":"1"});
            var Q1117;
            Q1117=makeQuery(id+"F12.opPattern","COPY",BODY,{"derivedFrom":makeQuery(id+"F10.opPattern","COPY",BODY,{"derivedFrom":makeQuery(id+"F9.opPattern","COPY",BODY,{"derivedFrom":makeQuery(id+"F8.opPattern","COPY",BODY,{"derivedFrom":makeQuery(id+"F6.opPattern","COPY",BODY,{"derivedFrom":makeQuery(id+"F2.opPattern","COPY",BODY,{"derivedFrom":makeQuery(id+"F1.opRevolve","SWEPT_BODY",BODY,{"disambiguationData":[OSD([sQuery(id+"F0.wireOp",EDGE,"E1")])]}),"instanceName":"1"}),"instanceName":"1"}),"instanceName":"1"}),"instanceName":"1"}),"instanceName":"1"}),"instanceName":"1"});
            var Q1118;
            Q1118=makeQuery(id+"F12.opPattern","COPY",BODY,{"derivedFrom":makeQuery(id+"F10.opPattern","COPY",BODY,{"derivedFrom":makeQuery(id+"F9.opPattern","COPY",BODY,{"derivedFrom":makeQuery(id+"F8.opPattern","COPY",BODY,{"derivedFrom":makeQuery(id+"F6.opPattern","COPY",BODY,{"derivedFrom":makeQuery(id+"F3.opPattern","COPY",BODY,{"derivedFrom":makeQuery(id+"F2.opPattern","COPY",BODY,{"derivedFrom":makeQuery(id+"F1.opRevolve","SWEPT_BODY",BODY,{"disambiguationData":[OSD([sQuery(id+"F0.wireOp",EDGE,"E1")])]}),"instanceName":"1"}),"instanceName":"1"}),"instanceName":"1"}),"instanceName":"1"}),"instanceName":"1"}),"instanceName":"1"}),"instanceName":"1"});
            var Q1119;
            Q1119=makeQuery(id+"F12.opPattern","COPY",BODY,{"derivedFrom":makeQuery(id+"F10.opPattern","COPY",BODY,{"derivedFrom":makeQuery(id+"F9.opPattern","COPY",BODY,{"derivedFrom":makeQuery(id+"F8.opPattern","COPY",BODY,{"derivedFrom":makeQuery(id+"F6.opPattern","COPY",BODY,{"derivedFrom":makeQuery(id+"F4.opPattern","COPY",BODY,{"derivedFrom":makeQuery(id+"F1.opRevolve","SWEPT_BODY",BODY,{"disambiguationData":[OSD([sQuery(id+"F0.wireOp",EDGE,"E1")])]}),"instanceName":"1"}),"instanceName":"1"}),"instanceName":"1"}),"instanceName":"1"}),"instanceName":"1"}),"instanceName":"1"});
            var Q1120;
            Q1120=makeQuery(id+"F12.opPattern","COPY",BODY,{"derivedFrom":makeQuery(id+"F10.opPattern","COPY",BODY,{"derivedFrom":makeQuery(id+"F9.opPattern","COPY",BODY,{"derivedFrom":makeQuery(id+"F8.opPattern","COPY",BODY,{"derivedFrom":makeQuery(id+"F6.opPattern","COPY",BODY,{"derivedFrom":makeQuery(id+"F4.opPattern","COPY",BODY,{"derivedFrom":makeQuery(id+"F2.opPattern","COPY",BODY,{"derivedFrom":makeQuery(id+"F1.opRevolve","SWEPT_BODY",BODY,{"disambiguationData":[OSD([sQuery(id+"F0.wireOp",EDGE,"E1")])]}),"instanceName":"1"}),"instanceName":"1"}),"instanceName":"1"}),"instanceName":"1"}),"instanceName":"1"}),"instanceName":"1"}),"instanceName":"1"});
            var Q1121;
            Q1121=makeQuery(id+"F12.opPattern","COPY",BODY,{"derivedFrom":makeQuery(id+"F10.opPattern","COPY",BODY,{"derivedFrom":makeQuery(id+"F9.opPattern","COPY",BODY,{"derivedFrom":makeQuery(id+"F8.opPattern","COPY",BODY,{"derivedFrom":makeQuery(id+"F6.opPattern","COPY",BODY,{"derivedFrom":makeQuery(id+"F4.opPattern","COPY",BODY,{"derivedFrom":makeQuery(id+"F3.opPattern","COPY",BODY,{"derivedFrom":makeQuery(id+"F2.opPattern","COPY",BODY,{"derivedFrom":makeQuery(id+"F1.opRevolve","SWEPT_BODY",BODY,{"disambiguationData":[OSD([sQuery(id+"F0.wireOp",EDGE,"E1")])]}),"instanceName":"1"}),"instanceName":"1"}),"instanceName":"1"}),"instanceName":"1"}),"instanceName":"1"}),"instanceName":"1"}),"instanceName":"1"}),"instanceName":"1"});
            var Q1122;
            Q1122=makeQuery(id+"F12.opPattern","COPY",BODY,{"derivedFrom":makeQuery(id+"F10.opPattern","COPY",BODY,{"derivedFrom":makeQuery(id+"F9.opPattern","COPY",BODY,{"derivedFrom":makeQuery(id+"F8.opPattern","COPY",BODY,{"derivedFrom":makeQuery(id+"F6.opPattern","COPY",BODY,{"derivedFrom":makeQuery(id+"F5.opPattern","COPY",BODY,{"derivedFrom":makeQuery(id+"F1.opRevolve","SWEPT_BODY",BODY,{"disambiguationData":[OSD([sQuery(id+"F0.wireOp",EDGE,"E1")])]}),"instanceName":"1"}),"instanceName":"1"}),"instanceName":"1"}),"instanceName":"1"}),"instanceName":"1"}),"instanceName":"1"});
            var Q1123;
            Q1123=makeQuery(id+"F12.opPattern","COPY",BODY,{"derivedFrom":makeQuery(id+"F10.opPattern","COPY",BODY,{"derivedFrom":makeQuery(id+"F9.opPattern","COPY",BODY,{"derivedFrom":makeQuery(id+"F8.opPattern","COPY",BODY,{"derivedFrom":makeQuery(id+"F6.opPattern","COPY",BODY,{"derivedFrom":makeQuery(id+"F5.opPattern","COPY",BODY,{"derivedFrom":makeQuery(id+"F2.opPattern","COPY",BODY,{"derivedFrom":makeQuery(id+"F1.opRevolve","SWEPT_BODY",BODY,{"disambiguationData":[OSD([sQuery(id+"F0.wireOp",EDGE,"E1")])]}),"instanceName":"1"}),"instanceName":"1"}),"instanceName":"1"}),"instanceName":"1"}),"instanceName":"1"}),"instanceName":"1"}),"instanceName":"1"});
            var Q1124;
            Q1124=makeQuery(id+"F12.opPattern","COPY",BODY,{"derivedFrom":makeQuery(id+"F10.opPattern","COPY",BODY,{"derivedFrom":makeQuery(id+"F9.opPattern","COPY",BODY,{"derivedFrom":makeQuery(id+"F8.opPattern","COPY",BODY,{"derivedFrom":makeQuery(id+"F6.opPattern","COPY",BODY,{"derivedFrom":makeQuery(id+"F5.opPattern","COPY",BODY,{"derivedFrom":makeQuery(id+"F3.opPattern","COPY",BODY,{"derivedFrom":makeQuery(id+"F2.opPattern","COPY",BODY,{"derivedFrom":makeQuery(id+"F1.opRevolve","SWEPT_BODY",BODY,{"disambiguationData":[OSD([sQuery(id+"F0.wireOp",EDGE,"E1")])]}),"instanceName":"1"}),"instanceName":"1"}),"instanceName":"1"}),"instanceName":"1"}),"instanceName":"1"}),"instanceName":"1"}),"instanceName":"1"}),"instanceName":"1"});
            var Q1125;
            Q1125=makeQuery(id+"F12.opPattern","COPY",BODY,{"derivedFrom":makeQuery(id+"F10.opPattern","COPY",BODY,{"derivedFrom":makeQuery(id+"F9.opPattern","COPY",BODY,{"derivedFrom":makeQuery(id+"F8.opPattern","COPY",BODY,{"derivedFrom":makeQuery(id+"F6.opPattern","COPY",BODY,{"derivedFrom":makeQuery(id+"F5.opPattern","COPY",BODY,{"derivedFrom":makeQuery(id+"F4.opPattern","COPY",BODY,{"derivedFrom":makeQuery(id+"F1.opRevolve","SWEPT_BODY",BODY,{"disambiguationData":[OSD([sQuery(id+"F0.wireOp",EDGE,"E1")])]}),"instanceName":"1"}),"instanceName":"1"}),"instanceName":"1"}),"instanceName":"1"}),"instanceName":"1"}),"instanceName":"1"}),"instanceName":"1"});
            var Q1126;
            Q1126=makeQuery(id+"F12.opPattern","COPY",BODY,{"derivedFrom":makeQuery(id+"F10.opPattern","COPY",BODY,{"derivedFrom":makeQuery(id+"F9.opPattern","COPY",BODY,{"derivedFrom":makeQuery(id+"F8.opPattern","COPY",BODY,{"derivedFrom":makeQuery(id+"F6.opPattern","COPY",BODY,{"derivedFrom":makeQuery(id+"F5.opPattern","COPY",BODY,{"derivedFrom":makeQuery(id+"F4.opPattern","COPY",BODY,{"derivedFrom":makeQuery(id+"F2.opPattern","COPY",BODY,{"derivedFrom":makeQuery(id+"F1.opRevolve","SWEPT_BODY",BODY,{"disambiguationData":[OSD([sQuery(id+"F0.wireOp",EDGE,"E1")])]}),"instanceName":"1"}),"instanceName":"1"}),"instanceName":"1"}),"instanceName":"1"}),"instanceName":"1"}),"instanceName":"1"}),"instanceName":"1"}),"instanceName":"1"});
            var Q1127;
            Q1127=makeQuery(id+"F12.opPattern","COPY",BODY,{"derivedFrom":makeQuery(id+"F10.opPattern","COPY",BODY,{"derivedFrom":makeQuery(id+"F9.opPattern","COPY",BODY,{"derivedFrom":makeQuery(id+"F8.opPattern","COPY",BODY,{"derivedFrom":makeQuery(id+"F6.opPattern","COPY",BODY,{"derivedFrom":makeQuery(id+"F5.opPattern","COPY",BODY,{"derivedFrom":makeQuery(id+"F4.opPattern","COPY",BODY,{"derivedFrom":makeQuery(id+"F3.opPattern","COPY",BODY,{"derivedFrom":makeQuery(id+"F2.opPattern","COPY",BODY,{"derivedFrom":makeQuery(id+"F1.opRevolve","SWEPT_BODY",BODY,{"disambiguationData":[OSD([sQuery(id+"F0.wireOp",EDGE,"E1")])]}),"instanceName":"1"}),"instanceName":"1"}),"instanceName":"1"}),"instanceName":"1"}),"instanceName":"1"}),"instanceName":"1"}),"instanceName":"1"}),"instanceName":"1"}),"instanceName":"1"});
            var Q1128;
            Q1128=makeQuery(id+"F12.opPattern","COPY",BODY,{"derivedFrom":makeQuery(id+"F10.opPattern","COPY",BODY,{"derivedFrom":makeQuery(id+"F9.opPattern","COPY",BODY,{"derivedFrom":makeQuery(id+"F8.opPattern","COPY",BODY,{"derivedFrom":makeQuery(id+"F7.opPattern","COPY",BODY,{"derivedFrom":makeQuery(id+"F1.opRevolve","SWEPT_BODY",BODY,{"disambiguationData":[OSD([sQuery(id+"F0.wireOp",EDGE,"E1")])]}),"instanceName":"1"}),"instanceName":"1"}),"instanceName":"1"}),"instanceName":"1"}),"instanceName":"1"});
            var Q1129;
            Q1129=makeQuery(id+"F12.opPattern","COPY",BODY,{"derivedFrom":makeQuery(id+"F10.opPattern","COPY",BODY,{"derivedFrom":makeQuery(id+"F9.opPattern","COPY",BODY,{"derivedFrom":makeQuery(id+"F8.opPattern","COPY",BODY,{"derivedFrom":makeQuery(id+"F7.opPattern","COPY",BODY,{"derivedFrom":makeQuery(id+"F2.opPattern","COPY",BODY,{"derivedFrom":makeQuery(id+"F1.opRevolve","SWEPT_BODY",BODY,{"disambiguationData":[OSD([sQuery(id+"F0.wireOp",EDGE,"E1")])]}),"instanceName":"1"}),"instanceName":"1"}),"instanceName":"1"}),"instanceName":"1"}),"instanceName":"1"}),"instanceName":"1"});
            var Q1130;
            Q1130=makeQuery(id+"F12.opPattern","COPY",BODY,{"derivedFrom":makeQuery(id+"F10.opPattern","COPY",BODY,{"derivedFrom":makeQuery(id+"F9.opPattern","COPY",BODY,{"derivedFrom":makeQuery(id+"F8.opPattern","COPY",BODY,{"derivedFrom":makeQuery(id+"F7.opPattern","COPY",BODY,{"derivedFrom":makeQuery(id+"F3.opPattern","COPY",BODY,{"derivedFrom":makeQuery(id+"F2.opPattern","COPY",BODY,{"derivedFrom":makeQuery(id+"F1.opRevolve","SWEPT_BODY",BODY,{"disambiguationData":[OSD([sQuery(id+"F0.wireOp",EDGE,"E1")])]}),"instanceName":"1"}),"instanceName":"1"}),"instanceName":"1"}),"instanceName":"1"}),"instanceName":"1"}),"instanceName":"1"}),"instanceName":"1"});
            var Q1131;
            Q1131=makeQuery(id+"F12.opPattern","COPY",BODY,{"derivedFrom":makeQuery(id+"F10.opPattern","COPY",BODY,{"derivedFrom":makeQuery(id+"F9.opPattern","COPY",BODY,{"derivedFrom":makeQuery(id+"F8.opPattern","COPY",BODY,{"derivedFrom":makeQuery(id+"F7.opPattern","COPY",BODY,{"derivedFrom":makeQuery(id+"F4.opPattern","COPY",BODY,{"derivedFrom":makeQuery(id+"F1.opRevolve","SWEPT_BODY",BODY,{"disambiguationData":[OSD([sQuery(id+"F0.wireOp",EDGE,"E1")])]}),"instanceName":"1"}),"instanceName":"1"}),"instanceName":"1"}),"instanceName":"1"}),"instanceName":"1"}),"instanceName":"1"});
            var Q1132;
            Q1132=makeQuery(id+"F12.opPattern","COPY",BODY,{"derivedFrom":makeQuery(id+"F10.opPattern","COPY",BODY,{"derivedFrom":makeQuery(id+"F9.opPattern","COPY",BODY,{"derivedFrom":makeQuery(id+"F8.opPattern","COPY",BODY,{"derivedFrom":makeQuery(id+"F7.opPattern","COPY",BODY,{"derivedFrom":makeQuery(id+"F4.opPattern","COPY",BODY,{"derivedFrom":makeQuery(id+"F2.opPattern","COPY",BODY,{"derivedFrom":makeQuery(id+"F1.opRevolve","SWEPT_BODY",BODY,{"disambiguationData":[OSD([sQuery(id+"F0.wireOp",EDGE,"E1")])]}),"instanceName":"1"}),"instanceName":"1"}),"instanceName":"1"}),"instanceName":"1"}),"instanceName":"1"}),"instanceName":"1"}),"instanceName":"1"});
            var Q1133;
            Q1133=makeQuery(id+"F12.opPattern","COPY",BODY,{"derivedFrom":makeQuery(id+"F10.opPattern","COPY",BODY,{"derivedFrom":makeQuery(id+"F9.opPattern","COPY",BODY,{"derivedFrom":makeQuery(id+"F8.opPattern","COPY",BODY,{"derivedFrom":makeQuery(id+"F7.opPattern","COPY",BODY,{"derivedFrom":makeQuery(id+"F4.opPattern","COPY",BODY,{"derivedFrom":makeQuery(id+"F3.opPattern","COPY",BODY,{"derivedFrom":makeQuery(id+"F2.opPattern","COPY",BODY,{"derivedFrom":makeQuery(id+"F1.opRevolve","SWEPT_BODY",BODY,{"disambiguationData":[OSD([sQuery(id+"F0.wireOp",EDGE,"E1")])]}),"instanceName":"1"}),"instanceName":"1"}),"instanceName":"1"}),"instanceName":"1"}),"instanceName":"1"}),"instanceName":"1"}),"instanceName":"1"}),"instanceName":"1"});
            var Q1134;
            Q1134=makeQuery(id+"F12.opPattern","COPY",BODY,{"derivedFrom":makeQuery(id+"F10.opPattern","COPY",BODY,{"derivedFrom":makeQuery(id+"F9.opPattern","COPY",BODY,{"derivedFrom":makeQuery(id+"F8.opPattern","COPY",BODY,{"derivedFrom":makeQuery(id+"F7.opPattern","COPY",BODY,{"derivedFrom":makeQuery(id+"F5.opPattern","COPY",BODY,{"derivedFrom":makeQuery(id+"F1.opRevolve","SWEPT_BODY",BODY,{"disambiguationData":[OSD([sQuery(id+"F0.wireOp",EDGE,"E1")])]}),"instanceName":"1"}),"instanceName":"1"}),"instanceName":"1"}),"instanceName":"1"}),"instanceName":"1"}),"instanceName":"1"});
            var Q1135;
            Q1135=makeQuery(id+"F12.opPattern","COPY",BODY,{"derivedFrom":makeQuery(id+"F10.opPattern","COPY",BODY,{"derivedFrom":makeQuery(id+"F9.opPattern","COPY",BODY,{"derivedFrom":makeQuery(id+"F8.opPattern","COPY",BODY,{"derivedFrom":makeQuery(id+"F7.opPattern","COPY",BODY,{"derivedFrom":makeQuery(id+"F5.opPattern","COPY",BODY,{"derivedFrom":makeQuery(id+"F2.opPattern","COPY",BODY,{"derivedFrom":makeQuery(id+"F1.opRevolve","SWEPT_BODY",BODY,{"disambiguationData":[OSD([sQuery(id+"F0.wireOp",EDGE,"E1")])]}),"instanceName":"1"}),"instanceName":"1"}),"instanceName":"1"}),"instanceName":"1"}),"instanceName":"1"}),"instanceName":"1"}),"instanceName":"1"});
            var Q1136;
            Q1136=makeQuery(id+"F12.opPattern","COPY",BODY,{"derivedFrom":makeQuery(id+"F10.opPattern","COPY",BODY,{"derivedFrom":makeQuery(id+"F9.opPattern","COPY",BODY,{"derivedFrom":makeQuery(id+"F8.opPattern","COPY",BODY,{"derivedFrom":makeQuery(id+"F7.opPattern","COPY",BODY,{"derivedFrom":makeQuery(id+"F5.opPattern","COPY",BODY,{"derivedFrom":makeQuery(id+"F3.opPattern","COPY",BODY,{"derivedFrom":makeQuery(id+"F2.opPattern","COPY",BODY,{"derivedFrom":makeQuery(id+"F1.opRevolve","SWEPT_BODY",BODY,{"disambiguationData":[OSD([sQuery(id+"F0.wireOp",EDGE,"E1")])]}),"instanceName":"1"}),"instanceName":"1"}),"instanceName":"1"}),"instanceName":"1"}),"instanceName":"1"}),"instanceName":"1"}),"instanceName":"1"}),"instanceName":"1"});
            var Q1137;
            Q1137=makeQuery(id+"F12.opPattern","COPY",BODY,{"derivedFrom":makeQuery(id+"F10.opPattern","COPY",BODY,{"derivedFrom":makeQuery(id+"F9.opPattern","COPY",BODY,{"derivedFrom":makeQuery(id+"F8.opPattern","COPY",BODY,{"derivedFrom":makeQuery(id+"F7.opPattern","COPY",BODY,{"derivedFrom":makeQuery(id+"F5.opPattern","COPY",BODY,{"derivedFrom":makeQuery(id+"F4.opPattern","COPY",BODY,{"derivedFrom":makeQuery(id+"F1.opRevolve","SWEPT_BODY",BODY,{"disambiguationData":[OSD([sQuery(id+"F0.wireOp",EDGE,"E1")])]}),"instanceName":"1"}),"instanceName":"1"}),"instanceName":"1"}),"instanceName":"1"}),"instanceName":"1"}),"instanceName":"1"}),"instanceName":"1"});
            var Q1138;
            Q1138=makeQuery(id+"F12.opPattern","COPY",BODY,{"derivedFrom":makeQuery(id+"F10.opPattern","COPY",BODY,{"derivedFrom":makeQuery(id+"F9.opPattern","COPY",BODY,{"derivedFrom":makeQuery(id+"F8.opPattern","COPY",BODY,{"derivedFrom":makeQuery(id+"F7.opPattern","COPY",BODY,{"derivedFrom":makeQuery(id+"F5.opPattern","COPY",BODY,{"derivedFrom":makeQuery(id+"F4.opPattern","COPY",BODY,{"derivedFrom":makeQuery(id+"F2.opPattern","COPY",BODY,{"derivedFrom":makeQuery(id+"F1.opRevolve","SWEPT_BODY",BODY,{"disambiguationData":[OSD([sQuery(id+"F0.wireOp",EDGE,"E1")])]}),"instanceName":"1"}),"instanceName":"1"}),"instanceName":"1"}),"instanceName":"1"}),"instanceName":"1"}),"instanceName":"1"}),"instanceName":"1"}),"instanceName":"1"});
            var Q1139;
            Q1139=makeQuery(id+"F12.opPattern","COPY",BODY,{"derivedFrom":makeQuery(id+"F10.opPattern","COPY",BODY,{"derivedFrom":makeQuery(id+"F9.opPattern","COPY",BODY,{"derivedFrom":makeQuery(id+"F8.opPattern","COPY",BODY,{"derivedFrom":makeQuery(id+"F7.opPattern","COPY",BODY,{"derivedFrom":makeQuery(id+"F5.opPattern","COPY",BODY,{"derivedFrom":makeQuery(id+"F4.opPattern","COPY",BODY,{"derivedFrom":makeQuery(id+"F3.opPattern","COPY",BODY,{"derivedFrom":makeQuery(id+"F2.opPattern","COPY",BODY,{"derivedFrom":makeQuery(id+"F1.opRevolve","SWEPT_BODY",BODY,{"disambiguationData":[OSD([sQuery(id+"F0.wireOp",EDGE,"E1")])]}),"instanceName":"1"}),"instanceName":"1"}),"instanceName":"1"}),"instanceName":"1"}),"instanceName":"1"}),"instanceName":"1"}),"instanceName":"1"}),"instanceName":"1"}),"instanceName":"1"});
            var Q1140;
            Q1140=makeQuery(id+"F12.opPattern","COPY",BODY,{"derivedFrom":makeQuery(id+"F10.opPattern","COPY",BODY,{"derivedFrom":makeQuery(id+"F9.opPattern","COPY",BODY,{"derivedFrom":makeQuery(id+"F8.opPattern","COPY",BODY,{"derivedFrom":makeQuery(id+"F7.opPattern","COPY",BODY,{"derivedFrom":makeQuery(id+"F6.opPattern","COPY",BODY,{"derivedFrom":makeQuery(id+"F1.opRevolve","SWEPT_BODY",BODY,{"disambiguationData":[OSD([sQuery(id+"F0.wireOp",EDGE,"E1")])]}),"instanceName":"1"}),"instanceName":"1"}),"instanceName":"1"}),"instanceName":"1"}),"instanceName":"1"}),"instanceName":"1"});
            var Q1141;
            Q1141=makeQuery(id+"F12.opPattern","COPY",BODY,{"derivedFrom":makeQuery(id+"F10.opPattern","COPY",BODY,{"derivedFrom":makeQuery(id+"F9.opPattern","COPY",BODY,{"derivedFrom":makeQuery(id+"F8.opPattern","COPY",BODY,{"derivedFrom":makeQuery(id+"F7.opPattern","COPY",BODY,{"derivedFrom":makeQuery(id+"F6.opPattern","COPY",BODY,{"derivedFrom":makeQuery(id+"F2.opPattern","COPY",BODY,{"derivedFrom":makeQuery(id+"F1.opRevolve","SWEPT_BODY",BODY,{"disambiguationData":[OSD([sQuery(id+"F0.wireOp",EDGE,"E1")])]}),"instanceName":"1"}),"instanceName":"1"}),"instanceName":"1"}),"instanceName":"1"}),"instanceName":"1"}),"instanceName":"1"}),"instanceName":"1"});
            var Q1142;
            Q1142=makeQuery(id+"F12.opPattern","COPY",BODY,{"derivedFrom":makeQuery(id+"F10.opPattern","COPY",BODY,{"derivedFrom":makeQuery(id+"F9.opPattern","COPY",BODY,{"derivedFrom":makeQuery(id+"F8.opPattern","COPY",BODY,{"derivedFrom":makeQuery(id+"F7.opPattern","COPY",BODY,{"derivedFrom":makeQuery(id+"F6.opPattern","COPY",BODY,{"derivedFrom":makeQuery(id+"F3.opPattern","COPY",BODY,{"derivedFrom":makeQuery(id+"F2.opPattern","COPY",BODY,{"derivedFrom":makeQuery(id+"F1.opRevolve","SWEPT_BODY",BODY,{"disambiguationData":[OSD([sQuery(id+"F0.wireOp",EDGE,"E1")])]}),"instanceName":"1"}),"instanceName":"1"}),"instanceName":"1"}),"instanceName":"1"}),"instanceName":"1"}),"instanceName":"1"}),"instanceName":"1"}),"instanceName":"1"});
            var Q1143;
            Q1143=makeQuery(id+"F12.opPattern","COPY",BODY,{"derivedFrom":makeQuery(id+"F10.opPattern","COPY",BODY,{"derivedFrom":makeQuery(id+"F9.opPattern","COPY",BODY,{"derivedFrom":makeQuery(id+"F8.opPattern","COPY",BODY,{"derivedFrom":makeQuery(id+"F7.opPattern","COPY",BODY,{"derivedFrom":makeQuery(id+"F6.opPattern","COPY",BODY,{"derivedFrom":makeQuery(id+"F4.opPattern","COPY",BODY,{"derivedFrom":makeQuery(id+"F1.opRevolve","SWEPT_BODY",BODY,{"disambiguationData":[OSD([sQuery(id+"F0.wireOp",EDGE,"E1")])]}),"instanceName":"1"}),"instanceName":"1"}),"instanceName":"1"}),"instanceName":"1"}),"instanceName":"1"}),"instanceName":"1"}),"instanceName":"1"});
            var Q1144;
            Q1144=makeQuery(id+"F12.opPattern","COPY",BODY,{"derivedFrom":makeQuery(id+"F10.opPattern","COPY",BODY,{"derivedFrom":makeQuery(id+"F9.opPattern","COPY",BODY,{"derivedFrom":makeQuery(id+"F8.opPattern","COPY",BODY,{"derivedFrom":makeQuery(id+"F7.opPattern","COPY",BODY,{"derivedFrom":makeQuery(id+"F6.opPattern","COPY",BODY,{"derivedFrom":makeQuery(id+"F4.opPattern","COPY",BODY,{"derivedFrom":makeQuery(id+"F2.opPattern","COPY",BODY,{"derivedFrom":makeQuery(id+"F1.opRevolve","SWEPT_BODY",BODY,{"disambiguationData":[OSD([sQuery(id+"F0.wireOp",EDGE,"E1")])]}),"instanceName":"1"}),"instanceName":"1"}),"instanceName":"1"}),"instanceName":"1"}),"instanceName":"1"}),"instanceName":"1"}),"instanceName":"1"}),"instanceName":"1"});
            var Q1145;
            Q1145=makeQuery(id+"F12.opPattern","COPY",BODY,{"derivedFrom":makeQuery(id+"F10.opPattern","COPY",BODY,{"derivedFrom":makeQuery(id+"F9.opPattern","COPY",BODY,{"derivedFrom":makeQuery(id+"F8.opPattern","COPY",BODY,{"derivedFrom":makeQuery(id+"F7.opPattern","COPY",BODY,{"derivedFrom":makeQuery(id+"F6.opPattern","COPY",BODY,{"derivedFrom":makeQuery(id+"F4.opPattern","COPY",BODY,{"derivedFrom":makeQuery(id+"F3.opPattern","COPY",BODY,{"derivedFrom":makeQuery(id+"F2.opPattern","COPY",BODY,{"derivedFrom":makeQuery(id+"F1.opRevolve","SWEPT_BODY",BODY,{"disambiguationData":[OSD([sQuery(id+"F0.wireOp",EDGE,"E1")])]}),"instanceName":"1"}),"instanceName":"1"}),"instanceName":"1"}),"instanceName":"1"}),"instanceName":"1"}),"instanceName":"1"}),"instanceName":"1"}),"instanceName":"1"}),"instanceName":"1"});
            var Q1146;
            Q1146=makeQuery(id+"F12.opPattern","COPY",BODY,{"derivedFrom":makeQuery(id+"F10.opPattern","COPY",BODY,{"derivedFrom":makeQuery(id+"F9.opPattern","COPY",BODY,{"derivedFrom":makeQuery(id+"F8.opPattern","COPY",BODY,{"derivedFrom":makeQuery(id+"F7.opPattern","COPY",BODY,{"derivedFrom":makeQuery(id+"F6.opPattern","COPY",BODY,{"derivedFrom":makeQuery(id+"F5.opPattern","COPY",BODY,{"derivedFrom":makeQuery(id+"F1.opRevolve","SWEPT_BODY",BODY,{"disambiguationData":[OSD([sQuery(id+"F0.wireOp",EDGE,"E1")])]}),"instanceName":"1"}),"instanceName":"1"}),"instanceName":"1"}),"instanceName":"1"}),"instanceName":"1"}),"instanceName":"1"}),"instanceName":"1"});
            var Q1147;
            Q1147=makeQuery(id+"F12.opPattern","COPY",BODY,{"derivedFrom":makeQuery(id+"F10.opPattern","COPY",BODY,{"derivedFrom":makeQuery(id+"F9.opPattern","COPY",BODY,{"derivedFrom":makeQuery(id+"F8.opPattern","COPY",BODY,{"derivedFrom":makeQuery(id+"F7.opPattern","COPY",BODY,{"derivedFrom":makeQuery(id+"F6.opPattern","COPY",BODY,{"derivedFrom":makeQuery(id+"F5.opPattern","COPY",BODY,{"derivedFrom":makeQuery(id+"F2.opPattern","COPY",BODY,{"derivedFrom":makeQuery(id+"F1.opRevolve","SWEPT_BODY",BODY,{"disambiguationData":[OSD([sQuery(id+"F0.wireOp",EDGE,"E1")])]}),"instanceName":"1"}),"instanceName":"1"}),"instanceName":"1"}),"instanceName":"1"}),"instanceName":"1"}),"instanceName":"1"}),"instanceName":"1"}),"instanceName":"1"});
            var Q1148;
            Q1148=makeQuery(id+"F12.opPattern","COPY",BODY,{"derivedFrom":makeQuery(id+"F10.opPattern","COPY",BODY,{"derivedFrom":makeQuery(id+"F9.opPattern","COPY",BODY,{"derivedFrom":makeQuery(id+"F8.opPattern","COPY",BODY,{"derivedFrom":makeQuery(id+"F7.opPattern","COPY",BODY,{"derivedFrom":makeQuery(id+"F6.opPattern","COPY",BODY,{"derivedFrom":makeQuery(id+"F5.opPattern","COPY",BODY,{"derivedFrom":makeQuery(id+"F3.opPattern","COPY",BODY,{"derivedFrom":makeQuery(id+"F2.opPattern","COPY",BODY,{"derivedFrom":makeQuery(id+"F1.opRevolve","SWEPT_BODY",BODY,{"disambiguationData":[OSD([sQuery(id+"F0.wireOp",EDGE,"E1")])]}),"instanceName":"1"}),"instanceName":"1"}),"instanceName":"1"}),"instanceName":"1"}),"instanceName":"1"}),"instanceName":"1"}),"instanceName":"1"}),"instanceName":"1"}),"instanceName":"1"});
            var Q1149;
            Q1149=makeQuery(id+"F12.opPattern","COPY",BODY,{"derivedFrom":makeQuery(id+"F10.opPattern","COPY",BODY,{"derivedFrom":makeQuery(id+"F9.opPattern","COPY",BODY,{"derivedFrom":makeQuery(id+"F8.opPattern","COPY",BODY,{"derivedFrom":makeQuery(id+"F7.opPattern","COPY",BODY,{"derivedFrom":makeQuery(id+"F6.opPattern","COPY",BODY,{"derivedFrom":makeQuery(id+"F5.opPattern","COPY",BODY,{"derivedFrom":makeQuery(id+"F4.opPattern","COPY",BODY,{"derivedFrom":makeQuery(id+"F1.opRevolve","SWEPT_BODY",BODY,{"disambiguationData":[OSD([sQuery(id+"F0.wireOp",EDGE,"E1")])]}),"instanceName":"1"}),"instanceName":"1"}),"instanceName":"1"}),"instanceName":"1"}),"instanceName":"1"}),"instanceName":"1"}),"instanceName":"1"}),"instanceName":"1"});
            var Q1150;
            Q1150=makeQuery(id+"F12.opPattern","COPY",BODY,{"derivedFrom":makeQuery(id+"F10.opPattern","COPY",BODY,{"derivedFrom":makeQuery(id+"F9.opPattern","COPY",BODY,{"derivedFrom":makeQuery(id+"F8.opPattern","COPY",BODY,{"derivedFrom":makeQuery(id+"F7.opPattern","COPY",BODY,{"derivedFrom":makeQuery(id+"F6.opPattern","COPY",BODY,{"derivedFrom":makeQuery(id+"F5.opPattern","COPY",BODY,{"derivedFrom":makeQuery(id+"F4.opPattern","COPY",BODY,{"derivedFrom":makeQuery(id+"F2.opPattern","COPY",BODY,{"derivedFrom":makeQuery(id+"F1.opRevolve","SWEPT_BODY",BODY,{"disambiguationData":[OSD([sQuery(id+"F0.wireOp",EDGE,"E1")])]}),"instanceName":"1"}),"instanceName":"1"}),"instanceName":"1"}),"instanceName":"1"}),"instanceName":"1"}),"instanceName":"1"}),"instanceName":"1"}),"instanceName":"1"}),"instanceName":"1"});
            var Q1151;
            Q1151=makeQuery(id+"F12.opPattern","COPY",BODY,{"derivedFrom":makeQuery(id+"F10.opPattern","COPY",BODY,{"derivedFrom":makeQuery(id+"F9.opPattern","COPY",BODY,{"derivedFrom":makeQuery(id+"F8.opPattern","COPY",BODY,{"derivedFrom":makeQuery(id+"F7.opPattern","COPY",BODY,{"derivedFrom":makeQuery(id+"F6.opPattern","COPY",BODY,{"derivedFrom":makeQuery(id+"F5.opPattern","COPY",BODY,{"derivedFrom":makeQuery(id+"F4.opPattern","COPY",BODY,{"derivedFrom":makeQuery(id+"F3.opPattern","COPY",BODY,{"derivedFrom":makeQuery(id+"F2.opPattern","COPY",BODY,{"derivedFrom":makeQuery(id+"F1.opRevolve","SWEPT_BODY",BODY,{"disambiguationData":[OSD([sQuery(id+"F0.wireOp",EDGE,"E1")])]}),"instanceName":"1"}),"instanceName":"1"}),"instanceName":"1"}),"instanceName":"1"}),"instanceName":"1"}),"instanceName":"1"}),"instanceName":"1"}),"instanceName":"1"}),"instanceName":"1"}),"instanceName":"1"});
            var Q1152;
            Q1152=makeQuery(id+"F12.opPattern","COPY",BODY,{"derivedFrom":makeQuery(id+"F11.opPattern","COPY",BODY,{"derivedFrom":makeQuery(id+"F1.opRevolve","SWEPT_BODY",BODY,{"disambiguationData":[OSD([sQuery(id+"F0.wireOp",EDGE,"E1")])]}),"instanceName":"1"}),"instanceName":"1"});
            var Q1153;
            Q1153=makeQuery(id+"F12.opPattern","COPY",BODY,{"derivedFrom":makeQuery(id+"F11.opPattern","COPY",BODY,{"derivedFrom":makeQuery(id+"F2.opPattern","COPY",BODY,{"derivedFrom":makeQuery(id+"F1.opRevolve","SWEPT_BODY",BODY,{"disambiguationData":[OSD([sQuery(id+"F0.wireOp",EDGE,"E1")])]}),"instanceName":"1"}),"instanceName":"1"}),"instanceName":"1"});
            var Q1154;
            Q1154=makeQuery(id+"F12.opPattern","COPY",BODY,{"derivedFrom":makeQuery(id+"F11.opPattern","COPY",BODY,{"derivedFrom":makeQuery(id+"F3.opPattern","COPY",BODY,{"derivedFrom":makeQuery(id+"F2.opPattern","COPY",BODY,{"derivedFrom":makeQuery(id+"F1.opRevolve","SWEPT_BODY",BODY,{"disambiguationData":[OSD([sQuery(id+"F0.wireOp",EDGE,"E1")])]}),"instanceName":"1"}),"instanceName":"1"}),"instanceName":"1"}),"instanceName":"1"});
            var Q1155;
            Q1155=makeQuery(id+"F12.opPattern","COPY",BODY,{"derivedFrom":makeQuery(id+"F11.opPattern","COPY",BODY,{"derivedFrom":makeQuery(id+"F4.opPattern","COPY",BODY,{"derivedFrom":makeQuery(id+"F1.opRevolve","SWEPT_BODY",BODY,{"disambiguationData":[OSD([sQuery(id+"F0.wireOp",EDGE,"E1")])]}),"instanceName":"1"}),"instanceName":"1"}),"instanceName":"1"});
            var Q1156;
            Q1156=makeQuery(id+"F12.opPattern","COPY",BODY,{"derivedFrom":makeQuery(id+"F11.opPattern","COPY",BODY,{"derivedFrom":makeQuery(id+"F4.opPattern","COPY",BODY,{"derivedFrom":makeQuery(id+"F2.opPattern","COPY",BODY,{"derivedFrom":makeQuery(id+"F1.opRevolve","SWEPT_BODY",BODY,{"disambiguationData":[OSD([sQuery(id+"F0.wireOp",EDGE,"E1")])]}),"instanceName":"1"}),"instanceName":"1"}),"instanceName":"1"}),"instanceName":"1"});
            var Q1157;
            Q1157=makeQuery(id+"F12.opPattern","COPY",BODY,{"derivedFrom":makeQuery(id+"F11.opPattern","COPY",BODY,{"derivedFrom":makeQuery(id+"F4.opPattern","COPY",BODY,{"derivedFrom":makeQuery(id+"F3.opPattern","COPY",BODY,{"derivedFrom":makeQuery(id+"F2.opPattern","COPY",BODY,{"derivedFrom":makeQuery(id+"F1.opRevolve","SWEPT_BODY",BODY,{"disambiguationData":[OSD([sQuery(id+"F0.wireOp",EDGE,"E1")])]}),"instanceName":"1"}),"instanceName":"1"}),"instanceName":"1"}),"instanceName":"1"}),"instanceName":"1"});
            var Q1158;
            Q1158=makeQuery(id+"F12.opPattern","COPY",BODY,{"derivedFrom":makeQuery(id+"F11.opPattern","COPY",BODY,{"derivedFrom":makeQuery(id+"F5.opPattern","COPY",BODY,{"derivedFrom":makeQuery(id+"F1.opRevolve","SWEPT_BODY",BODY,{"disambiguationData":[OSD([sQuery(id+"F0.wireOp",EDGE,"E1")])]}),"instanceName":"1"}),"instanceName":"1"}),"instanceName":"1"});
            var Q1159;
            Q1159=makeQuery(id+"F12.opPattern","COPY",BODY,{"derivedFrom":makeQuery(id+"F11.opPattern","COPY",BODY,{"derivedFrom":makeQuery(id+"F5.opPattern","COPY",BODY,{"derivedFrom":makeQuery(id+"F2.opPattern","COPY",BODY,{"derivedFrom":makeQuery(id+"F1.opRevolve","SWEPT_BODY",BODY,{"disambiguationData":[OSD([sQuery(id+"F0.wireOp",EDGE,"E1")])]}),"instanceName":"1"}),"instanceName":"1"}),"instanceName":"1"}),"instanceName":"1"});
            var Q1160;
            Q1160=makeQuery(id+"F12.opPattern","COPY",BODY,{"derivedFrom":makeQuery(id+"F11.opPattern","COPY",BODY,{"derivedFrom":makeQuery(id+"F5.opPattern","COPY",BODY,{"derivedFrom":makeQuery(id+"F3.opPattern","COPY",BODY,{"derivedFrom":makeQuery(id+"F2.opPattern","COPY",BODY,{"derivedFrom":makeQuery(id+"F1.opRevolve","SWEPT_BODY",BODY,{"disambiguationData":[OSD([sQuery(id+"F0.wireOp",EDGE,"E1")])]}),"instanceName":"1"}),"instanceName":"1"}),"instanceName":"1"}),"instanceName":"1"}),"instanceName":"1"});
            var Q1161;
            Q1161=makeQuery(id+"F12.opPattern","COPY",BODY,{"derivedFrom":makeQuery(id+"F11.opPattern","COPY",BODY,{"derivedFrom":makeQuery(id+"F5.opPattern","COPY",BODY,{"derivedFrom":makeQuery(id+"F4.opPattern","COPY",BODY,{"derivedFrom":makeQuery(id+"F1.opRevolve","SWEPT_BODY",BODY,{"disambiguationData":[OSD([sQuery(id+"F0.wireOp",EDGE,"E1")])]}),"instanceName":"1"}),"instanceName":"1"}),"instanceName":"1"}),"instanceName":"1"});
            var Q1162;
            Q1162=makeQuery(id+"F12.opPattern","COPY",BODY,{"derivedFrom":makeQuery(id+"F11.opPattern","COPY",BODY,{"derivedFrom":makeQuery(id+"F5.opPattern","COPY",BODY,{"derivedFrom":makeQuery(id+"F4.opPattern","COPY",BODY,{"derivedFrom":makeQuery(id+"F2.opPattern","COPY",BODY,{"derivedFrom":makeQuery(id+"F1.opRevolve","SWEPT_BODY",BODY,{"disambiguationData":[OSD([sQuery(id+"F0.wireOp",EDGE,"E1")])]}),"instanceName":"1"}),"instanceName":"1"}),"instanceName":"1"}),"instanceName":"1"}),"instanceName":"1"});
            var Q1163;
            Q1163=makeQuery(id+"F12.opPattern","COPY",BODY,{"derivedFrom":makeQuery(id+"F11.opPattern","COPY",BODY,{"derivedFrom":makeQuery(id+"F5.opPattern","COPY",BODY,{"derivedFrom":makeQuery(id+"F4.opPattern","COPY",BODY,{"derivedFrom":makeQuery(id+"F3.opPattern","COPY",BODY,{"derivedFrom":makeQuery(id+"F2.opPattern","COPY",BODY,{"derivedFrom":makeQuery(id+"F1.opRevolve","SWEPT_BODY",BODY,{"disambiguationData":[OSD([sQuery(id+"F0.wireOp",EDGE,"E1")])]}),"instanceName":"1"}),"instanceName":"1"}),"instanceName":"1"}),"instanceName":"1"}),"instanceName":"1"}),"instanceName":"1"});
            var Q1164;
            Q1164=makeQuery(id+"F12.opPattern","COPY",BODY,{"derivedFrom":makeQuery(id+"F11.opPattern","COPY",BODY,{"derivedFrom":makeQuery(id+"F6.opPattern","COPY",BODY,{"derivedFrom":makeQuery(id+"F1.opRevolve","SWEPT_BODY",BODY,{"disambiguationData":[OSD([sQuery(id+"F0.wireOp",EDGE,"E1")])]}),"instanceName":"1"}),"instanceName":"1"}),"instanceName":"1"});
            var Q1165;
            Q1165=makeQuery(id+"F12.opPattern","COPY",BODY,{"derivedFrom":makeQuery(id+"F11.opPattern","COPY",BODY,{"derivedFrom":makeQuery(id+"F6.opPattern","COPY",BODY,{"derivedFrom":makeQuery(id+"F2.opPattern","COPY",BODY,{"derivedFrom":makeQuery(id+"F1.opRevolve","SWEPT_BODY",BODY,{"disambiguationData":[OSD([sQuery(id+"F0.wireOp",EDGE,"E1")])]}),"instanceName":"1"}),"instanceName":"1"}),"instanceName":"1"}),"instanceName":"1"});
            var Q1166;
            Q1166=makeQuery(id+"F12.opPattern","COPY",BODY,{"derivedFrom":makeQuery(id+"F11.opPattern","COPY",BODY,{"derivedFrom":makeQuery(id+"F6.opPattern","COPY",BODY,{"derivedFrom":makeQuery(id+"F3.opPattern","COPY",BODY,{"derivedFrom":makeQuery(id+"F2.opPattern","COPY",BODY,{"derivedFrom":makeQuery(id+"F1.opRevolve","SWEPT_BODY",BODY,{"disambiguationData":[OSD([sQuery(id+"F0.wireOp",EDGE,"E1")])]}),"instanceName":"1"}),"instanceName":"1"}),"instanceName":"1"}),"instanceName":"1"}),"instanceName":"1"});
            var Q1167;
            Q1167=makeQuery(id+"F12.opPattern","COPY",BODY,{"derivedFrom":makeQuery(id+"F11.opPattern","COPY",BODY,{"derivedFrom":makeQuery(id+"F6.opPattern","COPY",BODY,{"derivedFrom":makeQuery(id+"F4.opPattern","COPY",BODY,{"derivedFrom":makeQuery(id+"F1.opRevolve","SWEPT_BODY",BODY,{"disambiguationData":[OSD([sQuery(id+"F0.wireOp",EDGE,"E1")])]}),"instanceName":"1"}),"instanceName":"1"}),"instanceName":"1"}),"instanceName":"1"});
            var Q1168;
            Q1168=makeQuery(id+"F12.opPattern","COPY",BODY,{"derivedFrom":makeQuery(id+"F11.opPattern","COPY",BODY,{"derivedFrom":makeQuery(id+"F6.opPattern","COPY",BODY,{"derivedFrom":makeQuery(id+"F4.opPattern","COPY",BODY,{"derivedFrom":makeQuery(id+"F2.opPattern","COPY",BODY,{"derivedFrom":makeQuery(id+"F1.opRevolve","SWEPT_BODY",BODY,{"disambiguationData":[OSD([sQuery(id+"F0.wireOp",EDGE,"E1")])]}),"instanceName":"1"}),"instanceName":"1"}),"instanceName":"1"}),"instanceName":"1"}),"instanceName":"1"});
            var Q1169;
            Q1169=makeQuery(id+"F12.opPattern","COPY",BODY,{"derivedFrom":makeQuery(id+"F11.opPattern","COPY",BODY,{"derivedFrom":makeQuery(id+"F6.opPattern","COPY",BODY,{"derivedFrom":makeQuery(id+"F4.opPattern","COPY",BODY,{"derivedFrom":makeQuery(id+"F3.opPattern","COPY",BODY,{"derivedFrom":makeQuery(id+"F2.opPattern","COPY",BODY,{"derivedFrom":makeQuery(id+"F1.opRevolve","SWEPT_BODY",BODY,{"disambiguationData":[OSD([sQuery(id+"F0.wireOp",EDGE,"E1")])]}),"instanceName":"1"}),"instanceName":"1"}),"instanceName":"1"}),"instanceName":"1"}),"instanceName":"1"}),"instanceName":"1"});
            var Q1170;
            Q1170=makeQuery(id+"F12.opPattern","COPY",BODY,{"derivedFrom":makeQuery(id+"F11.opPattern","COPY",BODY,{"derivedFrom":makeQuery(id+"F6.opPattern","COPY",BODY,{"derivedFrom":makeQuery(id+"F5.opPattern","COPY",BODY,{"derivedFrom":makeQuery(id+"F1.opRevolve","SWEPT_BODY",BODY,{"disambiguationData":[OSD([sQuery(id+"F0.wireOp",EDGE,"E1")])]}),"instanceName":"1"}),"instanceName":"1"}),"instanceName":"1"}),"instanceName":"1"});
            var Q1171;
            Q1171=makeQuery(id+"F12.opPattern","COPY",BODY,{"derivedFrom":makeQuery(id+"F11.opPattern","COPY",BODY,{"derivedFrom":makeQuery(id+"F6.opPattern","COPY",BODY,{"derivedFrom":makeQuery(id+"F5.opPattern","COPY",BODY,{"derivedFrom":makeQuery(id+"F2.opPattern","COPY",BODY,{"derivedFrom":makeQuery(id+"F1.opRevolve","SWEPT_BODY",BODY,{"disambiguationData":[OSD([sQuery(id+"F0.wireOp",EDGE,"E1")])]}),"instanceName":"1"}),"instanceName":"1"}),"instanceName":"1"}),"instanceName":"1"}),"instanceName":"1"});
            var Q1172;
            Q1172=makeQuery(id+"F12.opPattern","COPY",BODY,{"derivedFrom":makeQuery(id+"F11.opPattern","COPY",BODY,{"derivedFrom":makeQuery(id+"F6.opPattern","COPY",BODY,{"derivedFrom":makeQuery(id+"F5.opPattern","COPY",BODY,{"derivedFrom":makeQuery(id+"F3.opPattern","COPY",BODY,{"derivedFrom":makeQuery(id+"F2.opPattern","COPY",BODY,{"derivedFrom":makeQuery(id+"F1.opRevolve","SWEPT_BODY",BODY,{"disambiguationData":[OSD([sQuery(id+"F0.wireOp",EDGE,"E1")])]}),"instanceName":"1"}),"instanceName":"1"}),"instanceName":"1"}),"instanceName":"1"}),"instanceName":"1"}),"instanceName":"1"});
            var Q1173;
            Q1173=makeQuery(id+"F12.opPattern","COPY",BODY,{"derivedFrom":makeQuery(id+"F11.opPattern","COPY",BODY,{"derivedFrom":makeQuery(id+"F6.opPattern","COPY",BODY,{"derivedFrom":makeQuery(id+"F5.opPattern","COPY",BODY,{"derivedFrom":makeQuery(id+"F4.opPattern","COPY",BODY,{"derivedFrom":makeQuery(id+"F1.opRevolve","SWEPT_BODY",BODY,{"disambiguationData":[OSD([sQuery(id+"F0.wireOp",EDGE,"E1")])]}),"instanceName":"1"}),"instanceName":"1"}),"instanceName":"1"}),"instanceName":"1"}),"instanceName":"1"});
            var Q1174;
            Q1174=makeQuery(id+"F12.opPattern","COPY",BODY,{"derivedFrom":makeQuery(id+"F11.opPattern","COPY",BODY,{"derivedFrom":makeQuery(id+"F6.opPattern","COPY",BODY,{"derivedFrom":makeQuery(id+"F5.opPattern","COPY",BODY,{"derivedFrom":makeQuery(id+"F4.opPattern","COPY",BODY,{"derivedFrom":makeQuery(id+"F2.opPattern","COPY",BODY,{"derivedFrom":makeQuery(id+"F1.opRevolve","SWEPT_BODY",BODY,{"disambiguationData":[OSD([sQuery(id+"F0.wireOp",EDGE,"E1")])]}),"instanceName":"1"}),"instanceName":"1"}),"instanceName":"1"}),"instanceName":"1"}),"instanceName":"1"}),"instanceName":"1"});
            var Q1175;
            Q1175=makeQuery(id+"F12.opPattern","COPY",BODY,{"derivedFrom":makeQuery(id+"F11.opPattern","COPY",BODY,{"derivedFrom":makeQuery(id+"F6.opPattern","COPY",BODY,{"derivedFrom":makeQuery(id+"F5.opPattern","COPY",BODY,{"derivedFrom":makeQuery(id+"F4.opPattern","COPY",BODY,{"derivedFrom":makeQuery(id+"F3.opPattern","COPY",BODY,{"derivedFrom":makeQuery(id+"F2.opPattern","COPY",BODY,{"derivedFrom":makeQuery(id+"F1.opRevolve","SWEPT_BODY",BODY,{"disambiguationData":[OSD([sQuery(id+"F0.wireOp",EDGE,"E1")])]}),"instanceName":"1"}),"instanceName":"1"}),"instanceName":"1"}),"instanceName":"1"}),"instanceName":"1"}),"instanceName":"1"}),"instanceName":"1"});
            var Q1176;
            Q1176=makeQuery(id+"F12.opPattern","COPY",BODY,{"derivedFrom":makeQuery(id+"F11.opPattern","COPY",BODY,{"derivedFrom":makeQuery(id+"F7.opPattern","COPY",BODY,{"derivedFrom":makeQuery(id+"F1.opRevolve","SWEPT_BODY",BODY,{"disambiguationData":[OSD([sQuery(id+"F0.wireOp",EDGE,"E1")])]}),"instanceName":"1"}),"instanceName":"1"}),"instanceName":"1"});
            var Q1177;
            Q1177=makeQuery(id+"F12.opPattern","COPY",BODY,{"derivedFrom":makeQuery(id+"F11.opPattern","COPY",BODY,{"derivedFrom":makeQuery(id+"F7.opPattern","COPY",BODY,{"derivedFrom":makeQuery(id+"F2.opPattern","COPY",BODY,{"derivedFrom":makeQuery(id+"F1.opRevolve","SWEPT_BODY",BODY,{"disambiguationData":[OSD([sQuery(id+"F0.wireOp",EDGE,"E1")])]}),"instanceName":"1"}),"instanceName":"1"}),"instanceName":"1"}),"instanceName":"1"});
            var Q1178;
            Q1178=makeQuery(id+"F12.opPattern","COPY",BODY,{"derivedFrom":makeQuery(id+"F11.opPattern","COPY",BODY,{"derivedFrom":makeQuery(id+"F7.opPattern","COPY",BODY,{"derivedFrom":makeQuery(id+"F3.opPattern","COPY",BODY,{"derivedFrom":makeQuery(id+"F2.opPattern","COPY",BODY,{"derivedFrom":makeQuery(id+"F1.opRevolve","SWEPT_BODY",BODY,{"disambiguationData":[OSD([sQuery(id+"F0.wireOp",EDGE,"E1")])]}),"instanceName":"1"}),"instanceName":"1"}),"instanceName":"1"}),"instanceName":"1"}),"instanceName":"1"});
            var Q1179;
            Q1179=makeQuery(id+"F12.opPattern","COPY",BODY,{"derivedFrom":makeQuery(id+"F11.opPattern","COPY",BODY,{"derivedFrom":makeQuery(id+"F7.opPattern","COPY",BODY,{"derivedFrom":makeQuery(id+"F4.opPattern","COPY",BODY,{"derivedFrom":makeQuery(id+"F1.opRevolve","SWEPT_BODY",BODY,{"disambiguationData":[OSD([sQuery(id+"F0.wireOp",EDGE,"E1")])]}),"instanceName":"1"}),"instanceName":"1"}),"instanceName":"1"}),"instanceName":"1"});
            var Q1180;
            Q1180=makeQuery(id+"F12.opPattern","COPY",BODY,{"derivedFrom":makeQuery(id+"F11.opPattern","COPY",BODY,{"derivedFrom":makeQuery(id+"F7.opPattern","COPY",BODY,{"derivedFrom":makeQuery(id+"F4.opPattern","COPY",BODY,{"derivedFrom":makeQuery(id+"F2.opPattern","COPY",BODY,{"derivedFrom":makeQuery(id+"F1.opRevolve","SWEPT_BODY",BODY,{"disambiguationData":[OSD([sQuery(id+"F0.wireOp",EDGE,"E1")])]}),"instanceName":"1"}),"instanceName":"1"}),"instanceName":"1"}),"instanceName":"1"}),"instanceName":"1"});
            var Q1181;
            Q1181=makeQuery(id+"F12.opPattern","COPY",BODY,{"derivedFrom":makeQuery(id+"F11.opPattern","COPY",BODY,{"derivedFrom":makeQuery(id+"F7.opPattern","COPY",BODY,{"derivedFrom":makeQuery(id+"F4.opPattern","COPY",BODY,{"derivedFrom":makeQuery(id+"F3.opPattern","COPY",BODY,{"derivedFrom":makeQuery(id+"F2.opPattern","COPY",BODY,{"derivedFrom":makeQuery(id+"F1.opRevolve","SWEPT_BODY",BODY,{"disambiguationData":[OSD([sQuery(id+"F0.wireOp",EDGE,"E1")])]}),"instanceName":"1"}),"instanceName":"1"}),"instanceName":"1"}),"instanceName":"1"}),"instanceName":"1"}),"instanceName":"1"});
            var Q1182;
            Q1182=makeQuery(id+"F12.opPattern","COPY",BODY,{"derivedFrom":makeQuery(id+"F11.opPattern","COPY",BODY,{"derivedFrom":makeQuery(id+"F7.opPattern","COPY",BODY,{"derivedFrom":makeQuery(id+"F5.opPattern","COPY",BODY,{"derivedFrom":makeQuery(id+"F1.opRevolve","SWEPT_BODY",BODY,{"disambiguationData":[OSD([sQuery(id+"F0.wireOp",EDGE,"E1")])]}),"instanceName":"1"}),"instanceName":"1"}),"instanceName":"1"}),"instanceName":"1"});
            var Q1183;
            Q1183=makeQuery(id+"F12.opPattern","COPY",BODY,{"derivedFrom":makeQuery(id+"F11.opPattern","COPY",BODY,{"derivedFrom":makeQuery(id+"F7.opPattern","COPY",BODY,{"derivedFrom":makeQuery(id+"F5.opPattern","COPY",BODY,{"derivedFrom":makeQuery(id+"F2.opPattern","COPY",BODY,{"derivedFrom":makeQuery(id+"F1.opRevolve","SWEPT_BODY",BODY,{"disambiguationData":[OSD([sQuery(id+"F0.wireOp",EDGE,"E1")])]}),"instanceName":"1"}),"instanceName":"1"}),"instanceName":"1"}),"instanceName":"1"}),"instanceName":"1"});
            var Q1184;
            Q1184=makeQuery(id+"F12.opPattern","COPY",BODY,{"derivedFrom":makeQuery(id+"F11.opPattern","COPY",BODY,{"derivedFrom":makeQuery(id+"F7.opPattern","COPY",BODY,{"derivedFrom":makeQuery(id+"F5.opPattern","COPY",BODY,{"derivedFrom":makeQuery(id+"F3.opPattern","COPY",BODY,{"derivedFrom":makeQuery(id+"F2.opPattern","COPY",BODY,{"derivedFrom":makeQuery(id+"F1.opRevolve","SWEPT_BODY",BODY,{"disambiguationData":[OSD([sQuery(id+"F0.wireOp",EDGE,"E1")])]}),"instanceName":"1"}),"instanceName":"1"}),"instanceName":"1"}),"instanceName":"1"}),"instanceName":"1"}),"instanceName":"1"});
            var Q1185;
            Q1185=makeQuery(id+"F12.opPattern","COPY",BODY,{"derivedFrom":makeQuery(id+"F11.opPattern","COPY",BODY,{"derivedFrom":makeQuery(id+"F7.opPattern","COPY",BODY,{"derivedFrom":makeQuery(id+"F5.opPattern","COPY",BODY,{"derivedFrom":makeQuery(id+"F4.opPattern","COPY",BODY,{"derivedFrom":makeQuery(id+"F1.opRevolve","SWEPT_BODY",BODY,{"disambiguationData":[OSD([sQuery(id+"F0.wireOp",EDGE,"E1")])]}),"instanceName":"1"}),"instanceName":"1"}),"instanceName":"1"}),"instanceName":"1"}),"instanceName":"1"});
            var Q1186;
            Q1186=makeQuery(id+"F12.opPattern","COPY",BODY,{"derivedFrom":makeQuery(id+"F11.opPattern","COPY",BODY,{"derivedFrom":makeQuery(id+"F7.opPattern","COPY",BODY,{"derivedFrom":makeQuery(id+"F5.opPattern","COPY",BODY,{"derivedFrom":makeQuery(id+"F4.opPattern","COPY",BODY,{"derivedFrom":makeQuery(id+"F2.opPattern","COPY",BODY,{"derivedFrom":makeQuery(id+"F1.opRevolve","SWEPT_BODY",BODY,{"disambiguationData":[OSD([sQuery(id+"F0.wireOp",EDGE,"E1")])]}),"instanceName":"1"}),"instanceName":"1"}),"instanceName":"1"}),"instanceName":"1"}),"instanceName":"1"}),"instanceName":"1"});
            var Q1187;
            Q1187=makeQuery(id+"F12.opPattern","COPY",BODY,{"derivedFrom":makeQuery(id+"F11.opPattern","COPY",BODY,{"derivedFrom":makeQuery(id+"F7.opPattern","COPY",BODY,{"derivedFrom":makeQuery(id+"F5.opPattern","COPY",BODY,{"derivedFrom":makeQuery(id+"F4.opPattern","COPY",BODY,{"derivedFrom":makeQuery(id+"F3.opPattern","COPY",BODY,{"derivedFrom":makeQuery(id+"F2.opPattern","COPY",BODY,{"derivedFrom":makeQuery(id+"F1.opRevolve","SWEPT_BODY",BODY,{"disambiguationData":[OSD([sQuery(id+"F0.wireOp",EDGE,"E1")])]}),"instanceName":"1"}),"instanceName":"1"}),"instanceName":"1"}),"instanceName":"1"}),"instanceName":"1"}),"instanceName":"1"}),"instanceName":"1"});
            var Q1188;
            Q1188=makeQuery(id+"F12.opPattern","COPY",BODY,{"derivedFrom":makeQuery(id+"F11.opPattern","COPY",BODY,{"derivedFrom":makeQuery(id+"F7.opPattern","COPY",BODY,{"derivedFrom":makeQuery(id+"F6.opPattern","COPY",BODY,{"derivedFrom":makeQuery(id+"F1.opRevolve","SWEPT_BODY",BODY,{"disambiguationData":[OSD([sQuery(id+"F0.wireOp",EDGE,"E1")])]}),"instanceName":"1"}),"instanceName":"1"}),"instanceName":"1"}),"instanceName":"1"});
            var Q1189;
            Q1189=makeQuery(id+"F12.opPattern","COPY",BODY,{"derivedFrom":makeQuery(id+"F11.opPattern","COPY",BODY,{"derivedFrom":makeQuery(id+"F7.opPattern","COPY",BODY,{"derivedFrom":makeQuery(id+"F6.opPattern","COPY",BODY,{"derivedFrom":makeQuery(id+"F2.opPattern","COPY",BODY,{"derivedFrom":makeQuery(id+"F1.opRevolve","SWEPT_BODY",BODY,{"disambiguationData":[OSD([sQuery(id+"F0.wireOp",EDGE,"E1")])]}),"instanceName":"1"}),"instanceName":"1"}),"instanceName":"1"}),"instanceName":"1"}),"instanceName":"1"});
            var Q1190;
            Q1190=makeQuery(id+"F12.opPattern","COPY",BODY,{"derivedFrom":makeQuery(id+"F11.opPattern","COPY",BODY,{"derivedFrom":makeQuery(id+"F7.opPattern","COPY",BODY,{"derivedFrom":makeQuery(id+"F6.opPattern","COPY",BODY,{"derivedFrom":makeQuery(id+"F3.opPattern","COPY",BODY,{"derivedFrom":makeQuery(id+"F2.opPattern","COPY",BODY,{"derivedFrom":makeQuery(id+"F1.opRevolve","SWEPT_BODY",BODY,{"disambiguationData":[OSD([sQuery(id+"F0.wireOp",EDGE,"E1")])]}),"instanceName":"1"}),"instanceName":"1"}),"instanceName":"1"}),"instanceName":"1"}),"instanceName":"1"}),"instanceName":"1"});
            var Q1191;
            Q1191=makeQuery(id+"F12.opPattern","COPY",BODY,{"derivedFrom":makeQuery(id+"F11.opPattern","COPY",BODY,{"derivedFrom":makeQuery(id+"F7.opPattern","COPY",BODY,{"derivedFrom":makeQuery(id+"F6.opPattern","COPY",BODY,{"derivedFrom":makeQuery(id+"F4.opPattern","COPY",BODY,{"derivedFrom":makeQuery(id+"F1.opRevolve","SWEPT_BODY",BODY,{"disambiguationData":[OSD([sQuery(id+"F0.wireOp",EDGE,"E1")])]}),"instanceName":"1"}),"instanceName":"1"}),"instanceName":"1"}),"instanceName":"1"}),"instanceName":"1"});
            var Q1192;
            Q1192=makeQuery(id+"F12.opPattern","COPY",BODY,{"derivedFrom":makeQuery(id+"F11.opPattern","COPY",BODY,{"derivedFrom":makeQuery(id+"F7.opPattern","COPY",BODY,{"derivedFrom":makeQuery(id+"F6.opPattern","COPY",BODY,{"derivedFrom":makeQuery(id+"F4.opPattern","COPY",BODY,{"derivedFrom":makeQuery(id+"F2.opPattern","COPY",BODY,{"derivedFrom":makeQuery(id+"F1.opRevolve","SWEPT_BODY",BODY,{"disambiguationData":[OSD([sQuery(id+"F0.wireOp",EDGE,"E1")])]}),"instanceName":"1"}),"instanceName":"1"}),"instanceName":"1"}),"instanceName":"1"}),"instanceName":"1"}),"instanceName":"1"});
            var Q1193;
            Q1193=makeQuery(id+"F12.opPattern","COPY",BODY,{"derivedFrom":makeQuery(id+"F11.opPattern","COPY",BODY,{"derivedFrom":makeQuery(id+"F7.opPattern","COPY",BODY,{"derivedFrom":makeQuery(id+"F6.opPattern","COPY",BODY,{"derivedFrom":makeQuery(id+"F4.opPattern","COPY",BODY,{"derivedFrom":makeQuery(id+"F3.opPattern","COPY",BODY,{"derivedFrom":makeQuery(id+"F2.opPattern","COPY",BODY,{"derivedFrom":makeQuery(id+"F1.opRevolve","SWEPT_BODY",BODY,{"disambiguationData":[OSD([sQuery(id+"F0.wireOp",EDGE,"E1")])]}),"instanceName":"1"}),"instanceName":"1"}),"instanceName":"1"}),"instanceName":"1"}),"instanceName":"1"}),"instanceName":"1"}),"instanceName":"1"});
            var Q1194;
            Q1194=makeQuery(id+"F12.opPattern","COPY",BODY,{"derivedFrom":makeQuery(id+"F11.opPattern","COPY",BODY,{"derivedFrom":makeQuery(id+"F7.opPattern","COPY",BODY,{"derivedFrom":makeQuery(id+"F6.opPattern","COPY",BODY,{"derivedFrom":makeQuery(id+"F5.opPattern","COPY",BODY,{"derivedFrom":makeQuery(id+"F1.opRevolve","SWEPT_BODY",BODY,{"disambiguationData":[OSD([sQuery(id+"F0.wireOp",EDGE,"E1")])]}),"instanceName":"1"}),"instanceName":"1"}),"instanceName":"1"}),"instanceName":"1"}),"instanceName":"1"});
            var Q1195;
            Q1195=makeQuery(id+"F12.opPattern","COPY",BODY,{"derivedFrom":makeQuery(id+"F11.opPattern","COPY",BODY,{"derivedFrom":makeQuery(id+"F7.opPattern","COPY",BODY,{"derivedFrom":makeQuery(id+"F6.opPattern","COPY",BODY,{"derivedFrom":makeQuery(id+"F5.opPattern","COPY",BODY,{"derivedFrom":makeQuery(id+"F2.opPattern","COPY",BODY,{"derivedFrom":makeQuery(id+"F1.opRevolve","SWEPT_BODY",BODY,{"disambiguationData":[OSD([sQuery(id+"F0.wireOp",EDGE,"E1")])]}),"instanceName":"1"}),"instanceName":"1"}),"instanceName":"1"}),"instanceName":"1"}),"instanceName":"1"}),"instanceName":"1"});
            var Q1196;
            Q1196=makeQuery(id+"F12.opPattern","COPY",BODY,{"derivedFrom":makeQuery(id+"F11.opPattern","COPY",BODY,{"derivedFrom":makeQuery(id+"F7.opPattern","COPY",BODY,{"derivedFrom":makeQuery(id+"F6.opPattern","COPY",BODY,{"derivedFrom":makeQuery(id+"F5.opPattern","COPY",BODY,{"derivedFrom":makeQuery(id+"F3.opPattern","COPY",BODY,{"derivedFrom":makeQuery(id+"F2.opPattern","COPY",BODY,{"derivedFrom":makeQuery(id+"F1.opRevolve","SWEPT_BODY",BODY,{"disambiguationData":[OSD([sQuery(id+"F0.wireOp",EDGE,"E1")])]}),"instanceName":"1"}),"instanceName":"1"}),"instanceName":"1"}),"instanceName":"1"}),"instanceName":"1"}),"instanceName":"1"}),"instanceName":"1"});
            var Q1197;
            Q1197=makeQuery(id+"F12.opPattern","COPY",BODY,{"derivedFrom":makeQuery(id+"F11.opPattern","COPY",BODY,{"derivedFrom":makeQuery(id+"F7.opPattern","COPY",BODY,{"derivedFrom":makeQuery(id+"F6.opPattern","COPY",BODY,{"derivedFrom":makeQuery(id+"F5.opPattern","COPY",BODY,{"derivedFrom":makeQuery(id+"F4.opPattern","COPY",BODY,{"derivedFrom":makeQuery(id+"F1.opRevolve","SWEPT_BODY",BODY,{"disambiguationData":[OSD([sQuery(id+"F0.wireOp",EDGE,"E1")])]}),"instanceName":"1"}),"instanceName":"1"}),"instanceName":"1"}),"instanceName":"1"}),"instanceName":"1"}),"instanceName":"1"});
            var Q1198;
            Q1198=makeQuery(id+"F12.opPattern","COPY",BODY,{"derivedFrom":makeQuery(id+"F11.opPattern","COPY",BODY,{"derivedFrom":makeQuery(id+"F7.opPattern","COPY",BODY,{"derivedFrom":makeQuery(id+"F6.opPattern","COPY",BODY,{"derivedFrom":makeQuery(id+"F5.opPattern","COPY",BODY,{"derivedFrom":makeQuery(id+"F4.opPattern","COPY",BODY,{"derivedFrom":makeQuery(id+"F2.opPattern","COPY",BODY,{"derivedFrom":makeQuery(id+"F1.opRevolve","SWEPT_BODY",BODY,{"disambiguationData":[OSD([sQuery(id+"F0.wireOp",EDGE,"E1")])]}),"instanceName":"1"}),"instanceName":"1"}),"instanceName":"1"}),"instanceName":"1"}),"instanceName":"1"}),"instanceName":"1"}),"instanceName":"1"});
            var Q1199;
            Q1199=makeQuery(id+"F12.opPattern","COPY",BODY,{"derivedFrom":makeQuery(id+"F11.opPattern","COPY",BODY,{"derivedFrom":makeQuery(id+"F7.opPattern","COPY",BODY,{"derivedFrom":makeQuery(id+"F6.opPattern","COPY",BODY,{"derivedFrom":makeQuery(id+"F5.opPattern","COPY",BODY,{"derivedFrom":makeQuery(id+"F4.opPattern","COPY",BODY,{"derivedFrom":makeQuery(id+"F3.opPattern","COPY",BODY,{"derivedFrom":makeQuery(id+"F2.opPattern","COPY",BODY,{"derivedFrom":makeQuery(id+"F1.opRevolve","SWEPT_BODY",BODY,{"disambiguationData":[OSD([sQuery(id+"F0.wireOp",EDGE,"E1")])]}),"instanceName":"1"}),"instanceName":"1"}),"instanceName":"1"}),"instanceName":"1"}),"instanceName":"1"}),"instanceName":"1"}),"instanceName":"1"}),"instanceName":"1"});
            var Q1200;
            Q1200=makeQuery(id+"F12.opPattern","COPY",BODY,{"derivedFrom":makeQuery(id+"F11.opPattern","COPY",BODY,{"derivedFrom":makeQuery(id+"F8.opPattern","COPY",BODY,{"derivedFrom":makeQuery(id+"F1.opRevolve","SWEPT_BODY",BODY,{"disambiguationData":[OSD([sQuery(id+"F0.wireOp",EDGE,"E1")])]}),"instanceName":"1"}),"instanceName":"1"}),"instanceName":"1"});
            var Q1201;
            Q1201=makeQuery(id+"F12.opPattern","COPY",BODY,{"derivedFrom":makeQuery(id+"F11.opPattern","COPY",BODY,{"derivedFrom":makeQuery(id+"F8.opPattern","COPY",BODY,{"derivedFrom":makeQuery(id+"F2.opPattern","COPY",BODY,{"derivedFrom":makeQuery(id+"F1.opRevolve","SWEPT_BODY",BODY,{"disambiguationData":[OSD([sQuery(id+"F0.wireOp",EDGE,"E1")])]}),"instanceName":"1"}),"instanceName":"1"}),"instanceName":"1"}),"instanceName":"1"});
            var Q1202;
            Q1202=makeQuery(id+"F12.opPattern","COPY",BODY,{"derivedFrom":makeQuery(id+"F11.opPattern","COPY",BODY,{"derivedFrom":makeQuery(id+"F8.opPattern","COPY",BODY,{"derivedFrom":makeQuery(id+"F3.opPattern","COPY",BODY,{"derivedFrom":makeQuery(id+"F2.opPattern","COPY",BODY,{"derivedFrom":makeQuery(id+"F1.opRevolve","SWEPT_BODY",BODY,{"disambiguationData":[OSD([sQuery(id+"F0.wireOp",EDGE,"E1")])]}),"instanceName":"1"}),"instanceName":"1"}),"instanceName":"1"}),"instanceName":"1"}),"instanceName":"1"});
            var Q1203;
            Q1203=makeQuery(id+"F12.opPattern","COPY",BODY,{"derivedFrom":makeQuery(id+"F11.opPattern","COPY",BODY,{"derivedFrom":makeQuery(id+"F8.opPattern","COPY",BODY,{"derivedFrom":makeQuery(id+"F4.opPattern","COPY",BODY,{"derivedFrom":makeQuery(id+"F1.opRevolve","SWEPT_BODY",BODY,{"disambiguationData":[OSD([sQuery(id+"F0.wireOp",EDGE,"E1")])]}),"instanceName":"1"}),"instanceName":"1"}),"instanceName":"1"}),"instanceName":"1"});
            var Q1204;
            Q1204=makeQuery(id+"F12.opPattern","COPY",BODY,{"derivedFrom":makeQuery(id+"F11.opPattern","COPY",BODY,{"derivedFrom":makeQuery(id+"F8.opPattern","COPY",BODY,{"derivedFrom":makeQuery(id+"F4.opPattern","COPY",BODY,{"derivedFrom":makeQuery(id+"F2.opPattern","COPY",BODY,{"derivedFrom":makeQuery(id+"F1.opRevolve","SWEPT_BODY",BODY,{"disambiguationData":[OSD([sQuery(id+"F0.wireOp",EDGE,"E1")])]}),"instanceName":"1"}),"instanceName":"1"}),"instanceName":"1"}),"instanceName":"1"}),"instanceName":"1"});
            var Q1205;
            Q1205=makeQuery(id+"F12.opPattern","COPY",BODY,{"derivedFrom":makeQuery(id+"F11.opPattern","COPY",BODY,{"derivedFrom":makeQuery(id+"F8.opPattern","COPY",BODY,{"derivedFrom":makeQuery(id+"F4.opPattern","COPY",BODY,{"derivedFrom":makeQuery(id+"F3.opPattern","COPY",BODY,{"derivedFrom":makeQuery(id+"F2.opPattern","COPY",BODY,{"derivedFrom":makeQuery(id+"F1.opRevolve","SWEPT_BODY",BODY,{"disambiguationData":[OSD([sQuery(id+"F0.wireOp",EDGE,"E1")])]}),"instanceName":"1"}),"instanceName":"1"}),"instanceName":"1"}),"instanceName":"1"}),"instanceName":"1"}),"instanceName":"1"});
            var Q1206;
            Q1206=makeQuery(id+"F12.opPattern","COPY",BODY,{"derivedFrom":makeQuery(id+"F11.opPattern","COPY",BODY,{"derivedFrom":makeQuery(id+"F8.opPattern","COPY",BODY,{"derivedFrom":makeQuery(id+"F5.opPattern","COPY",BODY,{"derivedFrom":makeQuery(id+"F1.opRevolve","SWEPT_BODY",BODY,{"disambiguationData":[OSD([sQuery(id+"F0.wireOp",EDGE,"E1")])]}),"instanceName":"1"}),"instanceName":"1"}),"instanceName":"1"}),"instanceName":"1"});
            var Q1207;
            Q1207=makeQuery(id+"F12.opPattern","COPY",BODY,{"derivedFrom":makeQuery(id+"F11.opPattern","COPY",BODY,{"derivedFrom":makeQuery(id+"F8.opPattern","COPY",BODY,{"derivedFrom":makeQuery(id+"F5.opPattern","COPY",BODY,{"derivedFrom":makeQuery(id+"F2.opPattern","COPY",BODY,{"derivedFrom":makeQuery(id+"F1.opRevolve","SWEPT_BODY",BODY,{"disambiguationData":[OSD([sQuery(id+"F0.wireOp",EDGE,"E1")])]}),"instanceName":"1"}),"instanceName":"1"}),"instanceName":"1"}),"instanceName":"1"}),"instanceName":"1"});
            var Q1208;
            Q1208=makeQuery(id+"F12.opPattern","COPY",BODY,{"derivedFrom":makeQuery(id+"F11.opPattern","COPY",BODY,{"derivedFrom":makeQuery(id+"F8.opPattern","COPY",BODY,{"derivedFrom":makeQuery(id+"F5.opPattern","COPY",BODY,{"derivedFrom":makeQuery(id+"F3.opPattern","COPY",BODY,{"derivedFrom":makeQuery(id+"F2.opPattern","COPY",BODY,{"derivedFrom":makeQuery(id+"F1.opRevolve","SWEPT_BODY",BODY,{"disambiguationData":[OSD([sQuery(id+"F0.wireOp",EDGE,"E1")])]}),"instanceName":"1"}),"instanceName":"1"}),"instanceName":"1"}),"instanceName":"1"}),"instanceName":"1"}),"instanceName":"1"});
            var Q1209;
            Q1209=makeQuery(id+"F12.opPattern","COPY",BODY,{"derivedFrom":makeQuery(id+"F11.opPattern","COPY",BODY,{"derivedFrom":makeQuery(id+"F8.opPattern","COPY",BODY,{"derivedFrom":makeQuery(id+"F5.opPattern","COPY",BODY,{"derivedFrom":makeQuery(id+"F4.opPattern","COPY",BODY,{"derivedFrom":makeQuery(id+"F1.opRevolve","SWEPT_BODY",BODY,{"disambiguationData":[OSD([sQuery(id+"F0.wireOp",EDGE,"E1")])]}),"instanceName":"1"}),"instanceName":"1"}),"instanceName":"1"}),"instanceName":"1"}),"instanceName":"1"});
            var Q1210;
            Q1210=makeQuery(id+"F12.opPattern","COPY",BODY,{"derivedFrom":makeQuery(id+"F11.opPattern","COPY",BODY,{"derivedFrom":makeQuery(id+"F8.opPattern","COPY",BODY,{"derivedFrom":makeQuery(id+"F5.opPattern","COPY",BODY,{"derivedFrom":makeQuery(id+"F4.opPattern","COPY",BODY,{"derivedFrom":makeQuery(id+"F2.opPattern","COPY",BODY,{"derivedFrom":makeQuery(id+"F1.opRevolve","SWEPT_BODY",BODY,{"disambiguationData":[OSD([sQuery(id+"F0.wireOp",EDGE,"E1")])]}),"instanceName":"1"}),"instanceName":"1"}),"instanceName":"1"}),"instanceName":"1"}),"instanceName":"1"}),"instanceName":"1"});
            var Q1211;
            Q1211=makeQuery(id+"F12.opPattern","COPY",BODY,{"derivedFrom":makeQuery(id+"F11.opPattern","COPY",BODY,{"derivedFrom":makeQuery(id+"F8.opPattern","COPY",BODY,{"derivedFrom":makeQuery(id+"F5.opPattern","COPY",BODY,{"derivedFrom":makeQuery(id+"F4.opPattern","COPY",BODY,{"derivedFrom":makeQuery(id+"F3.opPattern","COPY",BODY,{"derivedFrom":makeQuery(id+"F2.opPattern","COPY",BODY,{"derivedFrom":makeQuery(id+"F1.opRevolve","SWEPT_BODY",BODY,{"disambiguationData":[OSD([sQuery(id+"F0.wireOp",EDGE,"E1")])]}),"instanceName":"1"}),"instanceName":"1"}),"instanceName":"1"}),"instanceName":"1"}),"instanceName":"1"}),"instanceName":"1"}),"instanceName":"1"});
            var Q1212;
            Q1212=makeQuery(id+"F12.opPattern","COPY",BODY,{"derivedFrom":makeQuery(id+"F11.opPattern","COPY",BODY,{"derivedFrom":makeQuery(id+"F8.opPattern","COPY",BODY,{"derivedFrom":makeQuery(id+"F6.opPattern","COPY",BODY,{"derivedFrom":makeQuery(id+"F1.opRevolve","SWEPT_BODY",BODY,{"disambiguationData":[OSD([sQuery(id+"F0.wireOp",EDGE,"E1")])]}),"instanceName":"1"}),"instanceName":"1"}),"instanceName":"1"}),"instanceName":"1"});
            var Q1213;
            Q1213=makeQuery(id+"F12.opPattern","COPY",BODY,{"derivedFrom":makeQuery(id+"F11.opPattern","COPY",BODY,{"derivedFrom":makeQuery(id+"F8.opPattern","COPY",BODY,{"derivedFrom":makeQuery(id+"F6.opPattern","COPY",BODY,{"derivedFrom":makeQuery(id+"F2.opPattern","COPY",BODY,{"derivedFrom":makeQuery(id+"F1.opRevolve","SWEPT_BODY",BODY,{"disambiguationData":[OSD([sQuery(id+"F0.wireOp",EDGE,"E1")])]}),"instanceName":"1"}),"instanceName":"1"}),"instanceName":"1"}),"instanceName":"1"}),"instanceName":"1"});
            var Q1214;
            Q1214=makeQuery(id+"F12.opPattern","COPY",BODY,{"derivedFrom":makeQuery(id+"F11.opPattern","COPY",BODY,{"derivedFrom":makeQuery(id+"F8.opPattern","COPY",BODY,{"derivedFrom":makeQuery(id+"F6.opPattern","COPY",BODY,{"derivedFrom":makeQuery(id+"F3.opPattern","COPY",BODY,{"derivedFrom":makeQuery(id+"F2.opPattern","COPY",BODY,{"derivedFrom":makeQuery(id+"F1.opRevolve","SWEPT_BODY",BODY,{"disambiguationData":[OSD([sQuery(id+"F0.wireOp",EDGE,"E1")])]}),"instanceName":"1"}),"instanceName":"1"}),"instanceName":"1"}),"instanceName":"1"}),"instanceName":"1"}),"instanceName":"1"});
            var Q1215;
            Q1215=makeQuery(id+"F12.opPattern","COPY",BODY,{"derivedFrom":makeQuery(id+"F11.opPattern","COPY",BODY,{"derivedFrom":makeQuery(id+"F8.opPattern","COPY",BODY,{"derivedFrom":makeQuery(id+"F6.opPattern","COPY",BODY,{"derivedFrom":makeQuery(id+"F4.opPattern","COPY",BODY,{"derivedFrom":makeQuery(id+"F1.opRevolve","SWEPT_BODY",BODY,{"disambiguationData":[OSD([sQuery(id+"F0.wireOp",EDGE,"E1")])]}),"instanceName":"1"}),"instanceName":"1"}),"instanceName":"1"}),"instanceName":"1"}),"instanceName":"1"});
            var Q1216;
            Q1216=makeQuery(id+"F12.opPattern","COPY",BODY,{"derivedFrom":makeQuery(id+"F11.opPattern","COPY",BODY,{"derivedFrom":makeQuery(id+"F8.opPattern","COPY",BODY,{"derivedFrom":makeQuery(id+"F6.opPattern","COPY",BODY,{"derivedFrom":makeQuery(id+"F4.opPattern","COPY",BODY,{"derivedFrom":makeQuery(id+"F2.opPattern","COPY",BODY,{"derivedFrom":makeQuery(id+"F1.opRevolve","SWEPT_BODY",BODY,{"disambiguationData":[OSD([sQuery(id+"F0.wireOp",EDGE,"E1")])]}),"instanceName":"1"}),"instanceName":"1"}),"instanceName":"1"}),"instanceName":"1"}),"instanceName":"1"}),"instanceName":"1"});
            var Q1217;
            Q1217=makeQuery(id+"F12.opPattern","COPY",BODY,{"derivedFrom":makeQuery(id+"F11.opPattern","COPY",BODY,{"derivedFrom":makeQuery(id+"F8.opPattern","COPY",BODY,{"derivedFrom":makeQuery(id+"F6.opPattern","COPY",BODY,{"derivedFrom":makeQuery(id+"F4.opPattern","COPY",BODY,{"derivedFrom":makeQuery(id+"F3.opPattern","COPY",BODY,{"derivedFrom":makeQuery(id+"F2.opPattern","COPY",BODY,{"derivedFrom":makeQuery(id+"F1.opRevolve","SWEPT_BODY",BODY,{"disambiguationData":[OSD([sQuery(id+"F0.wireOp",EDGE,"E1")])]}),"instanceName":"1"}),"instanceName":"1"}),"instanceName":"1"}),"instanceName":"1"}),"instanceName":"1"}),"instanceName":"1"}),"instanceName":"1"});
            var Q1218;
            Q1218=makeQuery(id+"F12.opPattern","COPY",BODY,{"derivedFrom":makeQuery(id+"F11.opPattern","COPY",BODY,{"derivedFrom":makeQuery(id+"F8.opPattern","COPY",BODY,{"derivedFrom":makeQuery(id+"F6.opPattern","COPY",BODY,{"derivedFrom":makeQuery(id+"F5.opPattern","COPY",BODY,{"derivedFrom":makeQuery(id+"F1.opRevolve","SWEPT_BODY",BODY,{"disambiguationData":[OSD([sQuery(id+"F0.wireOp",EDGE,"E1")])]}),"instanceName":"1"}),"instanceName":"1"}),"instanceName":"1"}),"instanceName":"1"}),"instanceName":"1"});
            var Q1219;
            Q1219=makeQuery(id+"F12.opPattern","COPY",BODY,{"derivedFrom":makeQuery(id+"F11.opPattern","COPY",BODY,{"derivedFrom":makeQuery(id+"F8.opPattern","COPY",BODY,{"derivedFrom":makeQuery(id+"F6.opPattern","COPY",BODY,{"derivedFrom":makeQuery(id+"F5.opPattern","COPY",BODY,{"derivedFrom":makeQuery(id+"F2.opPattern","COPY",BODY,{"derivedFrom":makeQuery(id+"F1.opRevolve","SWEPT_BODY",BODY,{"disambiguationData":[OSD([sQuery(id+"F0.wireOp",EDGE,"E1")])]}),"instanceName":"1"}),"instanceName":"1"}),"instanceName":"1"}),"instanceName":"1"}),"instanceName":"1"}),"instanceName":"1"});
            var Q1220;
            Q1220=makeQuery(id+"F12.opPattern","COPY",BODY,{"derivedFrom":makeQuery(id+"F11.opPattern","COPY",BODY,{"derivedFrom":makeQuery(id+"F8.opPattern","COPY",BODY,{"derivedFrom":makeQuery(id+"F6.opPattern","COPY",BODY,{"derivedFrom":makeQuery(id+"F5.opPattern","COPY",BODY,{"derivedFrom":makeQuery(id+"F3.opPattern","COPY",BODY,{"derivedFrom":makeQuery(id+"F2.opPattern","COPY",BODY,{"derivedFrom":makeQuery(id+"F1.opRevolve","SWEPT_BODY",BODY,{"disambiguationData":[OSD([sQuery(id+"F0.wireOp",EDGE,"E1")])]}),"instanceName":"1"}),"instanceName":"1"}),"instanceName":"1"}),"instanceName":"1"}),"instanceName":"1"}),"instanceName":"1"}),"instanceName":"1"});
            var Q1221;
            Q1221=makeQuery(id+"F12.opPattern","COPY",BODY,{"derivedFrom":makeQuery(id+"F11.opPattern","COPY",BODY,{"derivedFrom":makeQuery(id+"F8.opPattern","COPY",BODY,{"derivedFrom":makeQuery(id+"F6.opPattern","COPY",BODY,{"derivedFrom":makeQuery(id+"F5.opPattern","COPY",BODY,{"derivedFrom":makeQuery(id+"F4.opPattern","COPY",BODY,{"derivedFrom":makeQuery(id+"F1.opRevolve","SWEPT_BODY",BODY,{"disambiguationData":[OSD([sQuery(id+"F0.wireOp",EDGE,"E1")])]}),"instanceName":"1"}),"instanceName":"1"}),"instanceName":"1"}),"instanceName":"1"}),"instanceName":"1"}),"instanceName":"1"});
            var Q1222;
            Q1222=makeQuery(id+"F12.opPattern","COPY",BODY,{"derivedFrom":makeQuery(id+"F11.opPattern","COPY",BODY,{"derivedFrom":makeQuery(id+"F8.opPattern","COPY",BODY,{"derivedFrom":makeQuery(id+"F6.opPattern","COPY",BODY,{"derivedFrom":makeQuery(id+"F5.opPattern","COPY",BODY,{"derivedFrom":makeQuery(id+"F4.opPattern","COPY",BODY,{"derivedFrom":makeQuery(id+"F2.opPattern","COPY",BODY,{"derivedFrom":makeQuery(id+"F1.opRevolve","SWEPT_BODY",BODY,{"disambiguationData":[OSD([sQuery(id+"F0.wireOp",EDGE,"E1")])]}),"instanceName":"1"}),"instanceName":"1"}),"instanceName":"1"}),"instanceName":"1"}),"instanceName":"1"}),"instanceName":"1"}),"instanceName":"1"});
            var Q1223;
            Q1223=makeQuery(id+"F12.opPattern","COPY",BODY,{"derivedFrom":makeQuery(id+"F11.opPattern","COPY",BODY,{"derivedFrom":makeQuery(id+"F8.opPattern","COPY",BODY,{"derivedFrom":makeQuery(id+"F6.opPattern","COPY",BODY,{"derivedFrom":makeQuery(id+"F5.opPattern","COPY",BODY,{"derivedFrom":makeQuery(id+"F4.opPattern","COPY",BODY,{"derivedFrom":makeQuery(id+"F3.opPattern","COPY",BODY,{"derivedFrom":makeQuery(id+"F2.opPattern","COPY",BODY,{"derivedFrom":makeQuery(id+"F1.opRevolve","SWEPT_BODY",BODY,{"disambiguationData":[OSD([sQuery(id+"F0.wireOp",EDGE,"E1")])]}),"instanceName":"1"}),"instanceName":"1"}),"instanceName":"1"}),"instanceName":"1"}),"instanceName":"1"}),"instanceName":"1"}),"instanceName":"1"}),"instanceName":"1"});
            var Q1224;
            Q1224=makeQuery(id+"F12.opPattern","COPY",BODY,{"derivedFrom":makeQuery(id+"F11.opPattern","COPY",BODY,{"derivedFrom":makeQuery(id+"F8.opPattern","COPY",BODY,{"derivedFrom":makeQuery(id+"F7.opPattern","COPY",BODY,{"derivedFrom":makeQuery(id+"F1.opRevolve","SWEPT_BODY",BODY,{"disambiguationData":[OSD([sQuery(id+"F0.wireOp",EDGE,"E1")])]}),"instanceName":"1"}),"instanceName":"1"}),"instanceName":"1"}),"instanceName":"1"});
            var Q1225;
            Q1225=makeQuery(id+"F12.opPattern","COPY",BODY,{"derivedFrom":makeQuery(id+"F11.opPattern","COPY",BODY,{"derivedFrom":makeQuery(id+"F8.opPattern","COPY",BODY,{"derivedFrom":makeQuery(id+"F7.opPattern","COPY",BODY,{"derivedFrom":makeQuery(id+"F2.opPattern","COPY",BODY,{"derivedFrom":makeQuery(id+"F1.opRevolve","SWEPT_BODY",BODY,{"disambiguationData":[OSD([sQuery(id+"F0.wireOp",EDGE,"E1")])]}),"instanceName":"1"}),"instanceName":"1"}),"instanceName":"1"}),"instanceName":"1"}),"instanceName":"1"});
            var Q1226;
            Q1226=makeQuery(id+"F12.opPattern","COPY",BODY,{"derivedFrom":makeQuery(id+"F11.opPattern","COPY",BODY,{"derivedFrom":makeQuery(id+"F8.opPattern","COPY",BODY,{"derivedFrom":makeQuery(id+"F7.opPattern","COPY",BODY,{"derivedFrom":makeQuery(id+"F3.opPattern","COPY",BODY,{"derivedFrom":makeQuery(id+"F2.opPattern","COPY",BODY,{"derivedFrom":makeQuery(id+"F1.opRevolve","SWEPT_BODY",BODY,{"disambiguationData":[OSD([sQuery(id+"F0.wireOp",EDGE,"E1")])]}),"instanceName":"1"}),"instanceName":"1"}),"instanceName":"1"}),"instanceName":"1"}),"instanceName":"1"}),"instanceName":"1"});
            var Q1227;
            Q1227=makeQuery(id+"F12.opPattern","COPY",BODY,{"derivedFrom":makeQuery(id+"F11.opPattern","COPY",BODY,{"derivedFrom":makeQuery(id+"F8.opPattern","COPY",BODY,{"derivedFrom":makeQuery(id+"F7.opPattern","COPY",BODY,{"derivedFrom":makeQuery(id+"F4.opPattern","COPY",BODY,{"derivedFrom":makeQuery(id+"F1.opRevolve","SWEPT_BODY",BODY,{"disambiguationData":[OSD([sQuery(id+"F0.wireOp",EDGE,"E1")])]}),"instanceName":"1"}),"instanceName":"1"}),"instanceName":"1"}),"instanceName":"1"}),"instanceName":"1"});
            var Q1228;
            Q1228=makeQuery(id+"F12.opPattern","COPY",BODY,{"derivedFrom":makeQuery(id+"F11.opPattern","COPY",BODY,{"derivedFrom":makeQuery(id+"F8.opPattern","COPY",BODY,{"derivedFrom":makeQuery(id+"F7.opPattern","COPY",BODY,{"derivedFrom":makeQuery(id+"F4.opPattern","COPY",BODY,{"derivedFrom":makeQuery(id+"F2.opPattern","COPY",BODY,{"derivedFrom":makeQuery(id+"F1.opRevolve","SWEPT_BODY",BODY,{"disambiguationData":[OSD([sQuery(id+"F0.wireOp",EDGE,"E1")])]}),"instanceName":"1"}),"instanceName":"1"}),"instanceName":"1"}),"instanceName":"1"}),"instanceName":"1"}),"instanceName":"1"});
            var Q1229;
            Q1229=makeQuery(id+"F12.opPattern","COPY",BODY,{"derivedFrom":makeQuery(id+"F11.opPattern","COPY",BODY,{"derivedFrom":makeQuery(id+"F8.opPattern","COPY",BODY,{"derivedFrom":makeQuery(id+"F7.opPattern","COPY",BODY,{"derivedFrom":makeQuery(id+"F4.opPattern","COPY",BODY,{"derivedFrom":makeQuery(id+"F3.opPattern","COPY",BODY,{"derivedFrom":makeQuery(id+"F2.opPattern","COPY",BODY,{"derivedFrom":makeQuery(id+"F1.opRevolve","SWEPT_BODY",BODY,{"disambiguationData":[OSD([sQuery(id+"F0.wireOp",EDGE,"E1")])]}),"instanceName":"1"}),"instanceName":"1"}),"instanceName":"1"}),"instanceName":"1"}),"instanceName":"1"}),"instanceName":"1"}),"instanceName":"1"});
            var Q1230;
            Q1230=makeQuery(id+"F12.opPattern","COPY",BODY,{"derivedFrom":makeQuery(id+"F11.opPattern","COPY",BODY,{"derivedFrom":makeQuery(id+"F8.opPattern","COPY",BODY,{"derivedFrom":makeQuery(id+"F7.opPattern","COPY",BODY,{"derivedFrom":makeQuery(id+"F5.opPattern","COPY",BODY,{"derivedFrom":makeQuery(id+"F1.opRevolve","SWEPT_BODY",BODY,{"disambiguationData":[OSD([sQuery(id+"F0.wireOp",EDGE,"E1")])]}),"instanceName":"1"}),"instanceName":"1"}),"instanceName":"1"}),"instanceName":"1"}),"instanceName":"1"});
            var Q1231;
            Q1231=makeQuery(id+"F12.opPattern","COPY",BODY,{"derivedFrom":makeQuery(id+"F11.opPattern","COPY",BODY,{"derivedFrom":makeQuery(id+"F8.opPattern","COPY",BODY,{"derivedFrom":makeQuery(id+"F7.opPattern","COPY",BODY,{"derivedFrom":makeQuery(id+"F5.opPattern","COPY",BODY,{"derivedFrom":makeQuery(id+"F2.opPattern","COPY",BODY,{"derivedFrom":makeQuery(id+"F1.opRevolve","SWEPT_BODY",BODY,{"disambiguationData":[OSD([sQuery(id+"F0.wireOp",EDGE,"E1")])]}),"instanceName":"1"}),"instanceName":"1"}),"instanceName":"1"}),"instanceName":"1"}),"instanceName":"1"}),"instanceName":"1"});
            var Q1232;
            Q1232=makeQuery(id+"F12.opPattern","COPY",BODY,{"derivedFrom":makeQuery(id+"F11.opPattern","COPY",BODY,{"derivedFrom":makeQuery(id+"F8.opPattern","COPY",BODY,{"derivedFrom":makeQuery(id+"F7.opPattern","COPY",BODY,{"derivedFrom":makeQuery(id+"F5.opPattern","COPY",BODY,{"derivedFrom":makeQuery(id+"F3.opPattern","COPY",BODY,{"derivedFrom":makeQuery(id+"F2.opPattern","COPY",BODY,{"derivedFrom":makeQuery(id+"F1.opRevolve","SWEPT_BODY",BODY,{"disambiguationData":[OSD([sQuery(id+"F0.wireOp",EDGE,"E1")])]}),"instanceName":"1"}),"instanceName":"1"}),"instanceName":"1"}),"instanceName":"1"}),"instanceName":"1"}),"instanceName":"1"}),"instanceName":"1"});
            var Q1233;
            Q1233=makeQuery(id+"F12.opPattern","COPY",BODY,{"derivedFrom":makeQuery(id+"F11.opPattern","COPY",BODY,{"derivedFrom":makeQuery(id+"F8.opPattern","COPY",BODY,{"derivedFrom":makeQuery(id+"F7.opPattern","COPY",BODY,{"derivedFrom":makeQuery(id+"F5.opPattern","COPY",BODY,{"derivedFrom":makeQuery(id+"F4.opPattern","COPY",BODY,{"derivedFrom":makeQuery(id+"F1.opRevolve","SWEPT_BODY",BODY,{"disambiguationData":[OSD([sQuery(id+"F0.wireOp",EDGE,"E1")])]}),"instanceName":"1"}),"instanceName":"1"}),"instanceName":"1"}),"instanceName":"1"}),"instanceName":"1"}),"instanceName":"1"});
            var Q1234;
            Q1234=makeQuery(id+"F12.opPattern","COPY",BODY,{"derivedFrom":makeQuery(id+"F11.opPattern","COPY",BODY,{"derivedFrom":makeQuery(id+"F8.opPattern","COPY",BODY,{"derivedFrom":makeQuery(id+"F7.opPattern","COPY",BODY,{"derivedFrom":makeQuery(id+"F5.opPattern","COPY",BODY,{"derivedFrom":makeQuery(id+"F4.opPattern","COPY",BODY,{"derivedFrom":makeQuery(id+"F2.opPattern","COPY",BODY,{"derivedFrom":makeQuery(id+"F1.opRevolve","SWEPT_BODY",BODY,{"disambiguationData":[OSD([sQuery(id+"F0.wireOp",EDGE,"E1")])]}),"instanceName":"1"}),"instanceName":"1"}),"instanceName":"1"}),"instanceName":"1"}),"instanceName":"1"}),"instanceName":"1"}),"instanceName":"1"});
            var Q1235;
            Q1235=makeQuery(id+"F12.opPattern","COPY",BODY,{"derivedFrom":makeQuery(id+"F11.opPattern","COPY",BODY,{"derivedFrom":makeQuery(id+"F8.opPattern","COPY",BODY,{"derivedFrom":makeQuery(id+"F7.opPattern","COPY",BODY,{"derivedFrom":makeQuery(id+"F5.opPattern","COPY",BODY,{"derivedFrom":makeQuery(id+"F4.opPattern","COPY",BODY,{"derivedFrom":makeQuery(id+"F3.opPattern","COPY",BODY,{"derivedFrom":makeQuery(id+"F2.opPattern","COPY",BODY,{"derivedFrom":makeQuery(id+"F1.opRevolve","SWEPT_BODY",BODY,{"disambiguationData":[OSD([sQuery(id+"F0.wireOp",EDGE,"E1")])]}),"instanceName":"1"}),"instanceName":"1"}),"instanceName":"1"}),"instanceName":"1"}),"instanceName":"1"}),"instanceName":"1"}),"instanceName":"1"}),"instanceName":"1"});
            var Q1236;
            Q1236=makeQuery(id+"F12.opPattern","COPY",BODY,{"derivedFrom":makeQuery(id+"F11.opPattern","COPY",BODY,{"derivedFrom":makeQuery(id+"F8.opPattern","COPY",BODY,{"derivedFrom":makeQuery(id+"F7.opPattern","COPY",BODY,{"derivedFrom":makeQuery(id+"F6.opPattern","COPY",BODY,{"derivedFrom":makeQuery(id+"F1.opRevolve","SWEPT_BODY",BODY,{"disambiguationData":[OSD([sQuery(id+"F0.wireOp",EDGE,"E1")])]}),"instanceName":"1"}),"instanceName":"1"}),"instanceName":"1"}),"instanceName":"1"}),"instanceName":"1"});
            var Q1237;
            Q1237=makeQuery(id+"F12.opPattern","COPY",BODY,{"derivedFrom":makeQuery(id+"F11.opPattern","COPY",BODY,{"derivedFrom":makeQuery(id+"F8.opPattern","COPY",BODY,{"derivedFrom":makeQuery(id+"F7.opPattern","COPY",BODY,{"derivedFrom":makeQuery(id+"F6.opPattern","COPY",BODY,{"derivedFrom":makeQuery(id+"F2.opPattern","COPY",BODY,{"derivedFrom":makeQuery(id+"F1.opRevolve","SWEPT_BODY",BODY,{"disambiguationData":[OSD([sQuery(id+"F0.wireOp",EDGE,"E1")])]}),"instanceName":"1"}),"instanceName":"1"}),"instanceName":"1"}),"instanceName":"1"}),"instanceName":"1"}),"instanceName":"1"});
            var Q1238;
            Q1238=makeQuery(id+"F12.opPattern","COPY",BODY,{"derivedFrom":makeQuery(id+"F11.opPattern","COPY",BODY,{"derivedFrom":makeQuery(id+"F8.opPattern","COPY",BODY,{"derivedFrom":makeQuery(id+"F7.opPattern","COPY",BODY,{"derivedFrom":makeQuery(id+"F6.opPattern","COPY",BODY,{"derivedFrom":makeQuery(id+"F3.opPattern","COPY",BODY,{"derivedFrom":makeQuery(id+"F2.opPattern","COPY",BODY,{"derivedFrom":makeQuery(id+"F1.opRevolve","SWEPT_BODY",BODY,{"disambiguationData":[OSD([sQuery(id+"F0.wireOp",EDGE,"E1")])]}),"instanceName":"1"}),"instanceName":"1"}),"instanceName":"1"}),"instanceName":"1"}),"instanceName":"1"}),"instanceName":"1"}),"instanceName":"1"});
            var Q1239;
            Q1239=makeQuery(id+"F12.opPattern","COPY",BODY,{"derivedFrom":makeQuery(id+"F11.opPattern","COPY",BODY,{"derivedFrom":makeQuery(id+"F8.opPattern","COPY",BODY,{"derivedFrom":makeQuery(id+"F7.opPattern","COPY",BODY,{"derivedFrom":makeQuery(id+"F6.opPattern","COPY",BODY,{"derivedFrom":makeQuery(id+"F4.opPattern","COPY",BODY,{"derivedFrom":makeQuery(id+"F1.opRevolve","SWEPT_BODY",BODY,{"disambiguationData":[OSD([sQuery(id+"F0.wireOp",EDGE,"E1")])]}),"instanceName":"1"}),"instanceName":"1"}),"instanceName":"1"}),"instanceName":"1"}),"instanceName":"1"}),"instanceName":"1"});
            var Q1240;
            Q1240=makeQuery(id+"F12.opPattern","COPY",BODY,{"derivedFrom":makeQuery(id+"F11.opPattern","COPY",BODY,{"derivedFrom":makeQuery(id+"F8.opPattern","COPY",BODY,{"derivedFrom":makeQuery(id+"F7.opPattern","COPY",BODY,{"derivedFrom":makeQuery(id+"F6.opPattern","COPY",BODY,{"derivedFrom":makeQuery(id+"F4.opPattern","COPY",BODY,{"derivedFrom":makeQuery(id+"F2.opPattern","COPY",BODY,{"derivedFrom":makeQuery(id+"F1.opRevolve","SWEPT_BODY",BODY,{"disambiguationData":[OSD([sQuery(id+"F0.wireOp",EDGE,"E1")])]}),"instanceName":"1"}),"instanceName":"1"}),"instanceName":"1"}),"instanceName":"1"}),"instanceName":"1"}),"instanceName":"1"}),"instanceName":"1"});
            var Q1241;
            Q1241=makeQuery(id+"F12.opPattern","COPY",BODY,{"derivedFrom":makeQuery(id+"F11.opPattern","COPY",BODY,{"derivedFrom":makeQuery(id+"F8.opPattern","COPY",BODY,{"derivedFrom":makeQuery(id+"F7.opPattern","COPY",BODY,{"derivedFrom":makeQuery(id+"F6.opPattern","COPY",BODY,{"derivedFrom":makeQuery(id+"F4.opPattern","COPY",BODY,{"derivedFrom":makeQuery(id+"F3.opPattern","COPY",BODY,{"derivedFrom":makeQuery(id+"F2.opPattern","COPY",BODY,{"derivedFrom":makeQuery(id+"F1.opRevolve","SWEPT_BODY",BODY,{"disambiguationData":[OSD([sQuery(id+"F0.wireOp",EDGE,"E1")])]}),"instanceName":"1"}),"instanceName":"1"}),"instanceName":"1"}),"instanceName":"1"}),"instanceName":"1"}),"instanceName":"1"}),"instanceName":"1"}),"instanceName":"1"});
            var Q1242;
            Q1242=makeQuery(id+"F12.opPattern","COPY",BODY,{"derivedFrom":makeQuery(id+"F11.opPattern","COPY",BODY,{"derivedFrom":makeQuery(id+"F8.opPattern","COPY",BODY,{"derivedFrom":makeQuery(id+"F7.opPattern","COPY",BODY,{"derivedFrom":makeQuery(id+"F6.opPattern","COPY",BODY,{"derivedFrom":makeQuery(id+"F5.opPattern","COPY",BODY,{"derivedFrom":makeQuery(id+"F1.opRevolve","SWEPT_BODY",BODY,{"disambiguationData":[OSD([sQuery(id+"F0.wireOp",EDGE,"E1")])]}),"instanceName":"1"}),"instanceName":"1"}),"instanceName":"1"}),"instanceName":"1"}),"instanceName":"1"}),"instanceName":"1"});
            var Q1243;
            Q1243=makeQuery(id+"F12.opPattern","COPY",BODY,{"derivedFrom":makeQuery(id+"F11.opPattern","COPY",BODY,{"derivedFrom":makeQuery(id+"F8.opPattern","COPY",BODY,{"derivedFrom":makeQuery(id+"F7.opPattern","COPY",BODY,{"derivedFrom":makeQuery(id+"F6.opPattern","COPY",BODY,{"derivedFrom":makeQuery(id+"F5.opPattern","COPY",BODY,{"derivedFrom":makeQuery(id+"F2.opPattern","COPY",BODY,{"derivedFrom":makeQuery(id+"F1.opRevolve","SWEPT_BODY",BODY,{"disambiguationData":[OSD([sQuery(id+"F0.wireOp",EDGE,"E1")])]}),"instanceName":"1"}),"instanceName":"1"}),"instanceName":"1"}),"instanceName":"1"}),"instanceName":"1"}),"instanceName":"1"}),"instanceName":"1"});
            var Q1244;
            Q1244=makeQuery(id+"F12.opPattern","COPY",BODY,{"derivedFrom":makeQuery(id+"F11.opPattern","COPY",BODY,{"derivedFrom":makeQuery(id+"F8.opPattern","COPY",BODY,{"derivedFrom":makeQuery(id+"F7.opPattern","COPY",BODY,{"derivedFrom":makeQuery(id+"F6.opPattern","COPY",BODY,{"derivedFrom":makeQuery(id+"F5.opPattern","COPY",BODY,{"derivedFrom":makeQuery(id+"F3.opPattern","COPY",BODY,{"derivedFrom":makeQuery(id+"F2.opPattern","COPY",BODY,{"derivedFrom":makeQuery(id+"F1.opRevolve","SWEPT_BODY",BODY,{"disambiguationData":[OSD([sQuery(id+"F0.wireOp",EDGE,"E1")])]}),"instanceName":"1"}),"instanceName":"1"}),"instanceName":"1"}),"instanceName":"1"}),"instanceName":"1"}),"instanceName":"1"}),"instanceName":"1"}),"instanceName":"1"});
            var Q1245;
            Q1245=makeQuery(id+"F12.opPattern","COPY",BODY,{"derivedFrom":makeQuery(id+"F11.opPattern","COPY",BODY,{"derivedFrom":makeQuery(id+"F8.opPattern","COPY",BODY,{"derivedFrom":makeQuery(id+"F7.opPattern","COPY",BODY,{"derivedFrom":makeQuery(id+"F6.opPattern","COPY",BODY,{"derivedFrom":makeQuery(id+"F5.opPattern","COPY",BODY,{"derivedFrom":makeQuery(id+"F4.opPattern","COPY",BODY,{"derivedFrom":makeQuery(id+"F1.opRevolve","SWEPT_BODY",BODY,{"disambiguationData":[OSD([sQuery(id+"F0.wireOp",EDGE,"E1")])]}),"instanceName":"1"}),"instanceName":"1"}),"instanceName":"1"}),"instanceName":"1"}),"instanceName":"1"}),"instanceName":"1"}),"instanceName":"1"});
            var Q1246;
            Q1246=makeQuery(id+"F12.opPattern","COPY",BODY,{"derivedFrom":makeQuery(id+"F11.opPattern","COPY",BODY,{"derivedFrom":makeQuery(id+"F8.opPattern","COPY",BODY,{"derivedFrom":makeQuery(id+"F7.opPattern","COPY",BODY,{"derivedFrom":makeQuery(id+"F6.opPattern","COPY",BODY,{"derivedFrom":makeQuery(id+"F5.opPattern","COPY",BODY,{"derivedFrom":makeQuery(id+"F4.opPattern","COPY",BODY,{"derivedFrom":makeQuery(id+"F2.opPattern","COPY",BODY,{"derivedFrom":makeQuery(id+"F1.opRevolve","SWEPT_BODY",BODY,{"disambiguationData":[OSD([sQuery(id+"F0.wireOp",EDGE,"E1")])]}),"instanceName":"1"}),"instanceName":"1"}),"instanceName":"1"}),"instanceName":"1"}),"instanceName":"1"}),"instanceName":"1"}),"instanceName":"1"}),"instanceName":"1"});
            var Q1247;
            Q1247=makeQuery(id+"F12.opPattern","COPY",BODY,{"derivedFrom":makeQuery(id+"F11.opPattern","COPY",BODY,{"derivedFrom":makeQuery(id+"F8.opPattern","COPY",BODY,{"derivedFrom":makeQuery(id+"F7.opPattern","COPY",BODY,{"derivedFrom":makeQuery(id+"F6.opPattern","COPY",BODY,{"derivedFrom":makeQuery(id+"F5.opPattern","COPY",BODY,{"derivedFrom":makeQuery(id+"F4.opPattern","COPY",BODY,{"derivedFrom":makeQuery(id+"F3.opPattern","COPY",BODY,{"derivedFrom":makeQuery(id+"F2.opPattern","COPY",BODY,{"derivedFrom":makeQuery(id+"F1.opRevolve","SWEPT_BODY",BODY,{"disambiguationData":[OSD([sQuery(id+"F0.wireOp",EDGE,"E1")])]}),"instanceName":"1"}),"instanceName":"1"}),"instanceName":"1"}),"instanceName":"1"}),"instanceName":"1"}),"instanceName":"1"}),"instanceName":"1"}),"instanceName":"1"}),"instanceName":"1"});
            var Q1248;
            Q1248=makeQuery(id+"F12.opPattern","COPY",BODY,{"derivedFrom":makeQuery(id+"F11.opPattern","COPY",BODY,{"derivedFrom":makeQuery(id+"F9.opPattern","COPY",BODY,{"derivedFrom":makeQuery(id+"F1.opRevolve","SWEPT_BODY",BODY,{"disambiguationData":[OSD([sQuery(id+"F0.wireOp",EDGE,"E1")])]}),"instanceName":"1"}),"instanceName":"1"}),"instanceName":"1"});
            var Q1249;
            Q1249=makeQuery(id+"F12.opPattern","COPY",BODY,{"derivedFrom":makeQuery(id+"F11.opPattern","COPY",BODY,{"derivedFrom":makeQuery(id+"F9.opPattern","COPY",BODY,{"derivedFrom":makeQuery(id+"F2.opPattern","COPY",BODY,{"derivedFrom":makeQuery(id+"F1.opRevolve","SWEPT_BODY",BODY,{"disambiguationData":[OSD([sQuery(id+"F0.wireOp",EDGE,"E1")])]}),"instanceName":"1"}),"instanceName":"1"}),"instanceName":"1"}),"instanceName":"1"});
            var Q1250;
            Q1250=makeQuery(id+"F12.opPattern","COPY",BODY,{"derivedFrom":makeQuery(id+"F11.opPattern","COPY",BODY,{"derivedFrom":makeQuery(id+"F9.opPattern","COPY",BODY,{"derivedFrom":makeQuery(id+"F3.opPattern","COPY",BODY,{"derivedFrom":makeQuery(id+"F2.opPattern","COPY",BODY,{"derivedFrom":makeQuery(id+"F1.opRevolve","SWEPT_BODY",BODY,{"disambiguationData":[OSD([sQuery(id+"F0.wireOp",EDGE,"E1")])]}),"instanceName":"1"}),"instanceName":"1"}),"instanceName":"1"}),"instanceName":"1"}),"instanceName":"1"});
            var Q1251;
            Q1251=makeQuery(id+"F12.opPattern","COPY",BODY,{"derivedFrom":makeQuery(id+"F11.opPattern","COPY",BODY,{"derivedFrom":makeQuery(id+"F9.opPattern","COPY",BODY,{"derivedFrom":makeQuery(id+"F4.opPattern","COPY",BODY,{"derivedFrom":makeQuery(id+"F1.opRevolve","SWEPT_BODY",BODY,{"disambiguationData":[OSD([sQuery(id+"F0.wireOp",EDGE,"E1")])]}),"instanceName":"1"}),"instanceName":"1"}),"instanceName":"1"}),"instanceName":"1"});
            var Q1252;
            Q1252=makeQuery(id+"F12.opPattern","COPY",BODY,{"derivedFrom":makeQuery(id+"F11.opPattern","COPY",BODY,{"derivedFrom":makeQuery(id+"F9.opPattern","COPY",BODY,{"derivedFrom":makeQuery(id+"F4.opPattern","COPY",BODY,{"derivedFrom":makeQuery(id+"F2.opPattern","COPY",BODY,{"derivedFrom":makeQuery(id+"F1.opRevolve","SWEPT_BODY",BODY,{"disambiguationData":[OSD([sQuery(id+"F0.wireOp",EDGE,"E1")])]}),"instanceName":"1"}),"instanceName":"1"}),"instanceName":"1"}),"instanceName":"1"}),"instanceName":"1"});
            var Q1253;
            Q1253=makeQuery(id+"F12.opPattern","COPY",BODY,{"derivedFrom":makeQuery(id+"F11.opPattern","COPY",BODY,{"derivedFrom":makeQuery(id+"F9.opPattern","COPY",BODY,{"derivedFrom":makeQuery(id+"F4.opPattern","COPY",BODY,{"derivedFrom":makeQuery(id+"F3.opPattern","COPY",BODY,{"derivedFrom":makeQuery(id+"F2.opPattern","COPY",BODY,{"derivedFrom":makeQuery(id+"F1.opRevolve","SWEPT_BODY",BODY,{"disambiguationData":[OSD([sQuery(id+"F0.wireOp",EDGE,"E1")])]}),"instanceName":"1"}),"instanceName":"1"}),"instanceName":"1"}),"instanceName":"1"}),"instanceName":"1"}),"instanceName":"1"});
            var Q1254;
            Q1254=makeQuery(id+"F12.opPattern","COPY",BODY,{"derivedFrom":makeQuery(id+"F11.opPattern","COPY",BODY,{"derivedFrom":makeQuery(id+"F9.opPattern","COPY",BODY,{"derivedFrom":makeQuery(id+"F5.opPattern","COPY",BODY,{"derivedFrom":makeQuery(id+"F1.opRevolve","SWEPT_BODY",BODY,{"disambiguationData":[OSD([sQuery(id+"F0.wireOp",EDGE,"E1")])]}),"instanceName":"1"}),"instanceName":"1"}),"instanceName":"1"}),"instanceName":"1"});
            var Q1255;
            Q1255=makeQuery(id+"F12.opPattern","COPY",BODY,{"derivedFrom":makeQuery(id+"F11.opPattern","COPY",BODY,{"derivedFrom":makeQuery(id+"F9.opPattern","COPY",BODY,{"derivedFrom":makeQuery(id+"F5.opPattern","COPY",BODY,{"derivedFrom":makeQuery(id+"F2.opPattern","COPY",BODY,{"derivedFrom":makeQuery(id+"F1.opRevolve","SWEPT_BODY",BODY,{"disambiguationData":[OSD([sQuery(id+"F0.wireOp",EDGE,"E1")])]}),"instanceName":"1"}),"instanceName":"1"}),"instanceName":"1"}),"instanceName":"1"}),"instanceName":"1"});
            var Q1256;
            Q1256=makeQuery(id+"F12.opPattern","COPY",BODY,{"derivedFrom":makeQuery(id+"F11.opPattern","COPY",BODY,{"derivedFrom":makeQuery(id+"F9.opPattern","COPY",BODY,{"derivedFrom":makeQuery(id+"F5.opPattern","COPY",BODY,{"derivedFrom":makeQuery(id+"F3.opPattern","COPY",BODY,{"derivedFrom":makeQuery(id+"F2.opPattern","COPY",BODY,{"derivedFrom":makeQuery(id+"F1.opRevolve","SWEPT_BODY",BODY,{"disambiguationData":[OSD([sQuery(id+"F0.wireOp",EDGE,"E1")])]}),"instanceName":"1"}),"instanceName":"1"}),"instanceName":"1"}),"instanceName":"1"}),"instanceName":"1"}),"instanceName":"1"});
            var Q1257;
            Q1257=makeQuery(id+"F12.opPattern","COPY",BODY,{"derivedFrom":makeQuery(id+"F11.opPattern","COPY",BODY,{"derivedFrom":makeQuery(id+"F9.opPattern","COPY",BODY,{"derivedFrom":makeQuery(id+"F5.opPattern","COPY",BODY,{"derivedFrom":makeQuery(id+"F4.opPattern","COPY",BODY,{"derivedFrom":makeQuery(id+"F1.opRevolve","SWEPT_BODY",BODY,{"disambiguationData":[OSD([sQuery(id+"F0.wireOp",EDGE,"E1")])]}),"instanceName":"1"}),"instanceName":"1"}),"instanceName":"1"}),"instanceName":"1"}),"instanceName":"1"});
            var Q1258;
            Q1258=makeQuery(id+"F12.opPattern","COPY",BODY,{"derivedFrom":makeQuery(id+"F11.opPattern","COPY",BODY,{"derivedFrom":makeQuery(id+"F9.opPattern","COPY",BODY,{"derivedFrom":makeQuery(id+"F5.opPattern","COPY",BODY,{"derivedFrom":makeQuery(id+"F4.opPattern","COPY",BODY,{"derivedFrom":makeQuery(id+"F2.opPattern","COPY",BODY,{"derivedFrom":makeQuery(id+"F1.opRevolve","SWEPT_BODY",BODY,{"disambiguationData":[OSD([sQuery(id+"F0.wireOp",EDGE,"E1")])]}),"instanceName":"1"}),"instanceName":"1"}),"instanceName":"1"}),"instanceName":"1"}),"instanceName":"1"}),"instanceName":"1"});
            var Q1259;
            Q1259=makeQuery(id+"F12.opPattern","COPY",BODY,{"derivedFrom":makeQuery(id+"F11.opPattern","COPY",BODY,{"derivedFrom":makeQuery(id+"F9.opPattern","COPY",BODY,{"derivedFrom":makeQuery(id+"F5.opPattern","COPY",BODY,{"derivedFrom":makeQuery(id+"F4.opPattern","COPY",BODY,{"derivedFrom":makeQuery(id+"F3.opPattern","COPY",BODY,{"derivedFrom":makeQuery(id+"F2.opPattern","COPY",BODY,{"derivedFrom":makeQuery(id+"F1.opRevolve","SWEPT_BODY",BODY,{"disambiguationData":[OSD([sQuery(id+"F0.wireOp",EDGE,"E1")])]}),"instanceName":"1"}),"instanceName":"1"}),"instanceName":"1"}),"instanceName":"1"}),"instanceName":"1"}),"instanceName":"1"}),"instanceName":"1"});
            var Q1260;
            Q1260=makeQuery(id+"F12.opPattern","COPY",BODY,{"derivedFrom":makeQuery(id+"F11.opPattern","COPY",BODY,{"derivedFrom":makeQuery(id+"F9.opPattern","COPY",BODY,{"derivedFrom":makeQuery(id+"F6.opPattern","COPY",BODY,{"derivedFrom":makeQuery(id+"F1.opRevolve","SWEPT_BODY",BODY,{"disambiguationData":[OSD([sQuery(id+"F0.wireOp",EDGE,"E1")])]}),"instanceName":"1"}),"instanceName":"1"}),"instanceName":"1"}),"instanceName":"1"});
            var Q1261;
            Q1261=makeQuery(id+"F12.opPattern","COPY",BODY,{"derivedFrom":makeQuery(id+"F11.opPattern","COPY",BODY,{"derivedFrom":makeQuery(id+"F9.opPattern","COPY",BODY,{"derivedFrom":makeQuery(id+"F6.opPattern","COPY",BODY,{"derivedFrom":makeQuery(id+"F2.opPattern","COPY",BODY,{"derivedFrom":makeQuery(id+"F1.opRevolve","SWEPT_BODY",BODY,{"disambiguationData":[OSD([sQuery(id+"F0.wireOp",EDGE,"E1")])]}),"instanceName":"1"}),"instanceName":"1"}),"instanceName":"1"}),"instanceName":"1"}),"instanceName":"1"});
            var Q1262;
            Q1262=makeQuery(id+"F12.opPattern","COPY",BODY,{"derivedFrom":makeQuery(id+"F11.opPattern","COPY",BODY,{"derivedFrom":makeQuery(id+"F9.opPattern","COPY",BODY,{"derivedFrom":makeQuery(id+"F6.opPattern","COPY",BODY,{"derivedFrom":makeQuery(id+"F3.opPattern","COPY",BODY,{"derivedFrom":makeQuery(id+"F2.opPattern","COPY",BODY,{"derivedFrom":makeQuery(id+"F1.opRevolve","SWEPT_BODY",BODY,{"disambiguationData":[OSD([sQuery(id+"F0.wireOp",EDGE,"E1")])]}),"instanceName":"1"}),"instanceName":"1"}),"instanceName":"1"}),"instanceName":"1"}),"instanceName":"1"}),"instanceName":"1"});
            var Q1263;
            Q1263=makeQuery(id+"F12.opPattern","COPY",BODY,{"derivedFrom":makeQuery(id+"F11.opPattern","COPY",BODY,{"derivedFrom":makeQuery(id+"F9.opPattern","COPY",BODY,{"derivedFrom":makeQuery(id+"F6.opPattern","COPY",BODY,{"derivedFrom":makeQuery(id+"F4.opPattern","COPY",BODY,{"derivedFrom":makeQuery(id+"F1.opRevolve","SWEPT_BODY",BODY,{"disambiguationData":[OSD([sQuery(id+"F0.wireOp",EDGE,"E1")])]}),"instanceName":"1"}),"instanceName":"1"}),"instanceName":"1"}),"instanceName":"1"}),"instanceName":"1"});
            var Q1264;
            Q1264=makeQuery(id+"F12.opPattern","COPY",BODY,{"derivedFrom":makeQuery(id+"F11.opPattern","COPY",BODY,{"derivedFrom":makeQuery(id+"F9.opPattern","COPY",BODY,{"derivedFrom":makeQuery(id+"F6.opPattern","COPY",BODY,{"derivedFrom":makeQuery(id+"F4.opPattern","COPY",BODY,{"derivedFrom":makeQuery(id+"F2.opPattern","COPY",BODY,{"derivedFrom":makeQuery(id+"F1.opRevolve","SWEPT_BODY",BODY,{"disambiguationData":[OSD([sQuery(id+"F0.wireOp",EDGE,"E1")])]}),"instanceName":"1"}),"instanceName":"1"}),"instanceName":"1"}),"instanceName":"1"}),"instanceName":"1"}),"instanceName":"1"});
            var Q1265;
            Q1265=makeQuery(id+"F12.opPattern","COPY",BODY,{"derivedFrom":makeQuery(id+"F11.opPattern","COPY",BODY,{"derivedFrom":makeQuery(id+"F9.opPattern","COPY",BODY,{"derivedFrom":makeQuery(id+"F6.opPattern","COPY",BODY,{"derivedFrom":makeQuery(id+"F4.opPattern","COPY",BODY,{"derivedFrom":makeQuery(id+"F3.opPattern","COPY",BODY,{"derivedFrom":makeQuery(id+"F2.opPattern","COPY",BODY,{"derivedFrom":makeQuery(id+"F1.opRevolve","SWEPT_BODY",BODY,{"disambiguationData":[OSD([sQuery(id+"F0.wireOp",EDGE,"E1")])]}),"instanceName":"1"}),"instanceName":"1"}),"instanceName":"1"}),"instanceName":"1"}),"instanceName":"1"}),"instanceName":"1"}),"instanceName":"1"});
            var Q1266;
            Q1266=makeQuery(id+"F12.opPattern","COPY",BODY,{"derivedFrom":makeQuery(id+"F11.opPattern","COPY",BODY,{"derivedFrom":makeQuery(id+"F9.opPattern","COPY",BODY,{"derivedFrom":makeQuery(id+"F6.opPattern","COPY",BODY,{"derivedFrom":makeQuery(id+"F5.opPattern","COPY",BODY,{"derivedFrom":makeQuery(id+"F1.opRevolve","SWEPT_BODY",BODY,{"disambiguationData":[OSD([sQuery(id+"F0.wireOp",EDGE,"E1")])]}),"instanceName":"1"}),"instanceName":"1"}),"instanceName":"1"}),"instanceName":"1"}),"instanceName":"1"});
            var Q1267;
            Q1267=makeQuery(id+"F12.opPattern","COPY",BODY,{"derivedFrom":makeQuery(id+"F11.opPattern","COPY",BODY,{"derivedFrom":makeQuery(id+"F9.opPattern","COPY",BODY,{"derivedFrom":makeQuery(id+"F6.opPattern","COPY",BODY,{"derivedFrom":makeQuery(id+"F5.opPattern","COPY",BODY,{"derivedFrom":makeQuery(id+"F2.opPattern","COPY",BODY,{"derivedFrom":makeQuery(id+"F1.opRevolve","SWEPT_BODY",BODY,{"disambiguationData":[OSD([sQuery(id+"F0.wireOp",EDGE,"E1")])]}),"instanceName":"1"}),"instanceName":"1"}),"instanceName":"1"}),"instanceName":"1"}),"instanceName":"1"}),"instanceName":"1"});
            var Q1268;
            Q1268=makeQuery(id+"F12.opPattern","COPY",BODY,{"derivedFrom":makeQuery(id+"F11.opPattern","COPY",BODY,{"derivedFrom":makeQuery(id+"F9.opPattern","COPY",BODY,{"derivedFrom":makeQuery(id+"F6.opPattern","COPY",BODY,{"derivedFrom":makeQuery(id+"F5.opPattern","COPY",BODY,{"derivedFrom":makeQuery(id+"F3.opPattern","COPY",BODY,{"derivedFrom":makeQuery(id+"F2.opPattern","COPY",BODY,{"derivedFrom":makeQuery(id+"F1.opRevolve","SWEPT_BODY",BODY,{"disambiguationData":[OSD([sQuery(id+"F0.wireOp",EDGE,"E1")])]}),"instanceName":"1"}),"instanceName":"1"}),"instanceName":"1"}),"instanceName":"1"}),"instanceName":"1"}),"instanceName":"1"}),"instanceName":"1"});
            var Q1269;
            Q1269=makeQuery(id+"F12.opPattern","COPY",BODY,{"derivedFrom":makeQuery(id+"F11.opPattern","COPY",BODY,{"derivedFrom":makeQuery(id+"F9.opPattern","COPY",BODY,{"derivedFrom":makeQuery(id+"F6.opPattern","COPY",BODY,{"derivedFrom":makeQuery(id+"F5.opPattern","COPY",BODY,{"derivedFrom":makeQuery(id+"F4.opPattern","COPY",BODY,{"derivedFrom":makeQuery(id+"F1.opRevolve","SWEPT_BODY",BODY,{"disambiguationData":[OSD([sQuery(id+"F0.wireOp",EDGE,"E1")])]}),"instanceName":"1"}),"instanceName":"1"}),"instanceName":"1"}),"instanceName":"1"}),"instanceName":"1"}),"instanceName":"1"});
            var Q1270;
            Q1270=makeQuery(id+"F12.opPattern","COPY",BODY,{"derivedFrom":makeQuery(id+"F11.opPattern","COPY",BODY,{"derivedFrom":makeQuery(id+"F9.opPattern","COPY",BODY,{"derivedFrom":makeQuery(id+"F6.opPattern","COPY",BODY,{"derivedFrom":makeQuery(id+"F5.opPattern","COPY",BODY,{"derivedFrom":makeQuery(id+"F4.opPattern","COPY",BODY,{"derivedFrom":makeQuery(id+"F2.opPattern","COPY",BODY,{"derivedFrom":makeQuery(id+"F1.opRevolve","SWEPT_BODY",BODY,{"disambiguationData":[OSD([sQuery(id+"F0.wireOp",EDGE,"E1")])]}),"instanceName":"1"}),"instanceName":"1"}),"instanceName":"1"}),"instanceName":"1"}),"instanceName":"1"}),"instanceName":"1"}),"instanceName":"1"});
            var Q1271;
            Q1271=makeQuery(id+"F12.opPattern","COPY",BODY,{"derivedFrom":makeQuery(id+"F11.opPattern","COPY",BODY,{"derivedFrom":makeQuery(id+"F9.opPattern","COPY",BODY,{"derivedFrom":makeQuery(id+"F6.opPattern","COPY",BODY,{"derivedFrom":makeQuery(id+"F5.opPattern","COPY",BODY,{"derivedFrom":makeQuery(id+"F4.opPattern","COPY",BODY,{"derivedFrom":makeQuery(id+"F3.opPattern","COPY",BODY,{"derivedFrom":makeQuery(id+"F2.opPattern","COPY",BODY,{"derivedFrom":makeQuery(id+"F1.opRevolve","SWEPT_BODY",BODY,{"disambiguationData":[OSD([sQuery(id+"F0.wireOp",EDGE,"E1")])]}),"instanceName":"1"}),"instanceName":"1"}),"instanceName":"1"}),"instanceName":"1"}),"instanceName":"1"}),"instanceName":"1"}),"instanceName":"1"}),"instanceName":"1"});
            var Q1272;
            Q1272=makeQuery(id+"F12.opPattern","COPY",BODY,{"derivedFrom":makeQuery(id+"F11.opPattern","COPY",BODY,{"derivedFrom":makeQuery(id+"F9.opPattern","COPY",BODY,{"derivedFrom":makeQuery(id+"F7.opPattern","COPY",BODY,{"derivedFrom":makeQuery(id+"F1.opRevolve","SWEPT_BODY",BODY,{"disambiguationData":[OSD([sQuery(id+"F0.wireOp",EDGE,"E1")])]}),"instanceName":"1"}),"instanceName":"1"}),"instanceName":"1"}),"instanceName":"1"});
            var Q1273;
            Q1273=makeQuery(id+"F12.opPattern","COPY",BODY,{"derivedFrom":makeQuery(id+"F11.opPattern","COPY",BODY,{"derivedFrom":makeQuery(id+"F9.opPattern","COPY",BODY,{"derivedFrom":makeQuery(id+"F7.opPattern","COPY",BODY,{"derivedFrom":makeQuery(id+"F2.opPattern","COPY",BODY,{"derivedFrom":makeQuery(id+"F1.opRevolve","SWEPT_BODY",BODY,{"disambiguationData":[OSD([sQuery(id+"F0.wireOp",EDGE,"E1")])]}),"instanceName":"1"}),"instanceName":"1"}),"instanceName":"1"}),"instanceName":"1"}),"instanceName":"1"});
            var Q1274;
            Q1274=makeQuery(id+"F12.opPattern","COPY",BODY,{"derivedFrom":makeQuery(id+"F11.opPattern","COPY",BODY,{"derivedFrom":makeQuery(id+"F9.opPattern","COPY",BODY,{"derivedFrom":makeQuery(id+"F7.opPattern","COPY",BODY,{"derivedFrom":makeQuery(id+"F3.opPattern","COPY",BODY,{"derivedFrom":makeQuery(id+"F2.opPattern","COPY",BODY,{"derivedFrom":makeQuery(id+"F1.opRevolve","SWEPT_BODY",BODY,{"disambiguationData":[OSD([sQuery(id+"F0.wireOp",EDGE,"E1")])]}),"instanceName":"1"}),"instanceName":"1"}),"instanceName":"1"}),"instanceName":"1"}),"instanceName":"1"}),"instanceName":"1"});
            var Q1275;
            Q1275=makeQuery(id+"F12.opPattern","COPY",BODY,{"derivedFrom":makeQuery(id+"F11.opPattern","COPY",BODY,{"derivedFrom":makeQuery(id+"F9.opPattern","COPY",BODY,{"derivedFrom":makeQuery(id+"F7.opPattern","COPY",BODY,{"derivedFrom":makeQuery(id+"F4.opPattern","COPY",BODY,{"derivedFrom":makeQuery(id+"F1.opRevolve","SWEPT_BODY",BODY,{"disambiguationData":[OSD([sQuery(id+"F0.wireOp",EDGE,"E1")])]}),"instanceName":"1"}),"instanceName":"1"}),"instanceName":"1"}),"instanceName":"1"}),"instanceName":"1"});
            var Q1276;
            Q1276=makeQuery(id+"F12.opPattern","COPY",BODY,{"derivedFrom":makeQuery(id+"F11.opPattern","COPY",BODY,{"derivedFrom":makeQuery(id+"F9.opPattern","COPY",BODY,{"derivedFrom":makeQuery(id+"F7.opPattern","COPY",BODY,{"derivedFrom":makeQuery(id+"F4.opPattern","COPY",BODY,{"derivedFrom":makeQuery(id+"F2.opPattern","COPY",BODY,{"derivedFrom":makeQuery(id+"F1.opRevolve","SWEPT_BODY",BODY,{"disambiguationData":[OSD([sQuery(id+"F0.wireOp",EDGE,"E1")])]}),"instanceName":"1"}),"instanceName":"1"}),"instanceName":"1"}),"instanceName":"1"}),"instanceName":"1"}),"instanceName":"1"});
            var Q1277;
            Q1277=makeQuery(id+"F12.opPattern","COPY",BODY,{"derivedFrom":makeQuery(id+"F11.opPattern","COPY",BODY,{"derivedFrom":makeQuery(id+"F9.opPattern","COPY",BODY,{"derivedFrom":makeQuery(id+"F7.opPattern","COPY",BODY,{"derivedFrom":makeQuery(id+"F4.opPattern","COPY",BODY,{"derivedFrom":makeQuery(id+"F3.opPattern","COPY",BODY,{"derivedFrom":makeQuery(id+"F2.opPattern","COPY",BODY,{"derivedFrom":makeQuery(id+"F1.opRevolve","SWEPT_BODY",BODY,{"disambiguationData":[OSD([sQuery(id+"F0.wireOp",EDGE,"E1")])]}),"instanceName":"1"}),"instanceName":"1"}),"instanceName":"1"}),"instanceName":"1"}),"instanceName":"1"}),"instanceName":"1"}),"instanceName":"1"});
            var Q1278;
            Q1278=makeQuery(id+"F12.opPattern","COPY",BODY,{"derivedFrom":makeQuery(id+"F11.opPattern","COPY",BODY,{"derivedFrom":makeQuery(id+"F9.opPattern","COPY",BODY,{"derivedFrom":makeQuery(id+"F7.opPattern","COPY",BODY,{"derivedFrom":makeQuery(id+"F5.opPattern","COPY",BODY,{"derivedFrom":makeQuery(id+"F1.opRevolve","SWEPT_BODY",BODY,{"disambiguationData":[OSD([sQuery(id+"F0.wireOp",EDGE,"E1")])]}),"instanceName":"1"}),"instanceName":"1"}),"instanceName":"1"}),"instanceName":"1"}),"instanceName":"1"});
            var Q1279;
            Q1279=makeQuery(id+"F12.opPattern","COPY",BODY,{"derivedFrom":makeQuery(id+"F11.opPattern","COPY",BODY,{"derivedFrom":makeQuery(id+"F9.opPattern","COPY",BODY,{"derivedFrom":makeQuery(id+"F7.opPattern","COPY",BODY,{"derivedFrom":makeQuery(id+"F5.opPattern","COPY",BODY,{"derivedFrom":makeQuery(id+"F2.opPattern","COPY",BODY,{"derivedFrom":makeQuery(id+"F1.opRevolve","SWEPT_BODY",BODY,{"disambiguationData":[OSD([sQuery(id+"F0.wireOp",EDGE,"E1")])]}),"instanceName":"1"}),"instanceName":"1"}),"instanceName":"1"}),"instanceName":"1"}),"instanceName":"1"}),"instanceName":"1"});
            var Q1280;
            Q1280=makeQuery(id+"F12.opPattern","COPY",BODY,{"derivedFrom":makeQuery(id+"F11.opPattern","COPY",BODY,{"derivedFrom":makeQuery(id+"F9.opPattern","COPY",BODY,{"derivedFrom":makeQuery(id+"F7.opPattern","COPY",BODY,{"derivedFrom":makeQuery(id+"F5.opPattern","COPY",BODY,{"derivedFrom":makeQuery(id+"F3.opPattern","COPY",BODY,{"derivedFrom":makeQuery(id+"F2.opPattern","COPY",BODY,{"derivedFrom":makeQuery(id+"F1.opRevolve","SWEPT_BODY",BODY,{"disambiguationData":[OSD([sQuery(id+"F0.wireOp",EDGE,"E1")])]}),"instanceName":"1"}),"instanceName":"1"}),"instanceName":"1"}),"instanceName":"1"}),"instanceName":"1"}),"instanceName":"1"}),"instanceName":"1"});
            var Q1281;
            Q1281=makeQuery(id+"F12.opPattern","COPY",BODY,{"derivedFrom":makeQuery(id+"F11.opPattern","COPY",BODY,{"derivedFrom":makeQuery(id+"F9.opPattern","COPY",BODY,{"derivedFrom":makeQuery(id+"F7.opPattern","COPY",BODY,{"derivedFrom":makeQuery(id+"F5.opPattern","COPY",BODY,{"derivedFrom":makeQuery(id+"F4.opPattern","COPY",BODY,{"derivedFrom":makeQuery(id+"F1.opRevolve","SWEPT_BODY",BODY,{"disambiguationData":[OSD([sQuery(id+"F0.wireOp",EDGE,"E1")])]}),"instanceName":"1"}),"instanceName":"1"}),"instanceName":"1"}),"instanceName":"1"}),"instanceName":"1"}),"instanceName":"1"});
            var Q1282;
            Q1282=makeQuery(id+"F12.opPattern","COPY",BODY,{"derivedFrom":makeQuery(id+"F11.opPattern","COPY",BODY,{"derivedFrom":makeQuery(id+"F9.opPattern","COPY",BODY,{"derivedFrom":makeQuery(id+"F7.opPattern","COPY",BODY,{"derivedFrom":makeQuery(id+"F5.opPattern","COPY",BODY,{"derivedFrom":makeQuery(id+"F4.opPattern","COPY",BODY,{"derivedFrom":makeQuery(id+"F2.opPattern","COPY",BODY,{"derivedFrom":makeQuery(id+"F1.opRevolve","SWEPT_BODY",BODY,{"disambiguationData":[OSD([sQuery(id+"F0.wireOp",EDGE,"E1")])]}),"instanceName":"1"}),"instanceName":"1"}),"instanceName":"1"}),"instanceName":"1"}),"instanceName":"1"}),"instanceName":"1"}),"instanceName":"1"});
            var Q1283;
            Q1283=makeQuery(id+"F12.opPattern","COPY",BODY,{"derivedFrom":makeQuery(id+"F11.opPattern","COPY",BODY,{"derivedFrom":makeQuery(id+"F9.opPattern","COPY",BODY,{"derivedFrom":makeQuery(id+"F7.opPattern","COPY",BODY,{"derivedFrom":makeQuery(id+"F5.opPattern","COPY",BODY,{"derivedFrom":makeQuery(id+"F4.opPattern","COPY",BODY,{"derivedFrom":makeQuery(id+"F3.opPattern","COPY",BODY,{"derivedFrom":makeQuery(id+"F2.opPattern","COPY",BODY,{"derivedFrom":makeQuery(id+"F1.opRevolve","SWEPT_BODY",BODY,{"disambiguationData":[OSD([sQuery(id+"F0.wireOp",EDGE,"E1")])]}),"instanceName":"1"}),"instanceName":"1"}),"instanceName":"1"}),"instanceName":"1"}),"instanceName":"1"}),"instanceName":"1"}),"instanceName":"1"}),"instanceName":"1"});
            var Q1284;
            Q1284=makeQuery(id+"F12.opPattern","COPY",BODY,{"derivedFrom":makeQuery(id+"F11.opPattern","COPY",BODY,{"derivedFrom":makeQuery(id+"F9.opPattern","COPY",BODY,{"derivedFrom":makeQuery(id+"F7.opPattern","COPY",BODY,{"derivedFrom":makeQuery(id+"F6.opPattern","COPY",BODY,{"derivedFrom":makeQuery(id+"F1.opRevolve","SWEPT_BODY",BODY,{"disambiguationData":[OSD([sQuery(id+"F0.wireOp",EDGE,"E1")])]}),"instanceName":"1"}),"instanceName":"1"}),"instanceName":"1"}),"instanceName":"1"}),"instanceName":"1"});
            var Q1285;
            Q1285=makeQuery(id+"F12.opPattern","COPY",BODY,{"derivedFrom":makeQuery(id+"F11.opPattern","COPY",BODY,{"derivedFrom":makeQuery(id+"F9.opPattern","COPY",BODY,{"derivedFrom":makeQuery(id+"F7.opPattern","COPY",BODY,{"derivedFrom":makeQuery(id+"F6.opPattern","COPY",BODY,{"derivedFrom":makeQuery(id+"F2.opPattern","COPY",BODY,{"derivedFrom":makeQuery(id+"F1.opRevolve","SWEPT_BODY",BODY,{"disambiguationData":[OSD([sQuery(id+"F0.wireOp",EDGE,"E1")])]}),"instanceName":"1"}),"instanceName":"1"}),"instanceName":"1"}),"instanceName":"1"}),"instanceName":"1"}),"instanceName":"1"});
            var Q1286;
            Q1286=makeQuery(id+"F12.opPattern","COPY",BODY,{"derivedFrom":makeQuery(id+"F11.opPattern","COPY",BODY,{"derivedFrom":makeQuery(id+"F9.opPattern","COPY",BODY,{"derivedFrom":makeQuery(id+"F7.opPattern","COPY",BODY,{"derivedFrom":makeQuery(id+"F6.opPattern","COPY",BODY,{"derivedFrom":makeQuery(id+"F3.opPattern","COPY",BODY,{"derivedFrom":makeQuery(id+"F2.opPattern","COPY",BODY,{"derivedFrom":makeQuery(id+"F1.opRevolve","SWEPT_BODY",BODY,{"disambiguationData":[OSD([sQuery(id+"F0.wireOp",EDGE,"E1")])]}),"instanceName":"1"}),"instanceName":"1"}),"instanceName":"1"}),"instanceName":"1"}),"instanceName":"1"}),"instanceName":"1"}),"instanceName":"1"});
            var Q1287;
            Q1287=makeQuery(id+"F12.opPattern","COPY",BODY,{"derivedFrom":makeQuery(id+"F11.opPattern","COPY",BODY,{"derivedFrom":makeQuery(id+"F9.opPattern","COPY",BODY,{"derivedFrom":makeQuery(id+"F7.opPattern","COPY",BODY,{"derivedFrom":makeQuery(id+"F6.opPattern","COPY",BODY,{"derivedFrom":makeQuery(id+"F4.opPattern","COPY",BODY,{"derivedFrom":makeQuery(id+"F1.opRevolve","SWEPT_BODY",BODY,{"disambiguationData":[OSD([sQuery(id+"F0.wireOp",EDGE,"E1")])]}),"instanceName":"1"}),"instanceName":"1"}),"instanceName":"1"}),"instanceName":"1"}),"instanceName":"1"}),"instanceName":"1"});
            var Q1288;
            Q1288=makeQuery(id+"F12.opPattern","COPY",BODY,{"derivedFrom":makeQuery(id+"F11.opPattern","COPY",BODY,{"derivedFrom":makeQuery(id+"F9.opPattern","COPY",BODY,{"derivedFrom":makeQuery(id+"F7.opPattern","COPY",BODY,{"derivedFrom":makeQuery(id+"F6.opPattern","COPY",BODY,{"derivedFrom":makeQuery(id+"F4.opPattern","COPY",BODY,{"derivedFrom":makeQuery(id+"F2.opPattern","COPY",BODY,{"derivedFrom":makeQuery(id+"F1.opRevolve","SWEPT_BODY",BODY,{"disambiguationData":[OSD([sQuery(id+"F0.wireOp",EDGE,"E1")])]}),"instanceName":"1"}),"instanceName":"1"}),"instanceName":"1"}),"instanceName":"1"}),"instanceName":"1"}),"instanceName":"1"}),"instanceName":"1"});
            var Q1289;
            Q1289=makeQuery(id+"F12.opPattern","COPY",BODY,{"derivedFrom":makeQuery(id+"F11.opPattern","COPY",BODY,{"derivedFrom":makeQuery(id+"F9.opPattern","COPY",BODY,{"derivedFrom":makeQuery(id+"F7.opPattern","COPY",BODY,{"derivedFrom":makeQuery(id+"F6.opPattern","COPY",BODY,{"derivedFrom":makeQuery(id+"F4.opPattern","COPY",BODY,{"derivedFrom":makeQuery(id+"F3.opPattern","COPY",BODY,{"derivedFrom":makeQuery(id+"F2.opPattern","COPY",BODY,{"derivedFrom":makeQuery(id+"F1.opRevolve","SWEPT_BODY",BODY,{"disambiguationData":[OSD([sQuery(id+"F0.wireOp",EDGE,"E1")])]}),"instanceName":"1"}),"instanceName":"1"}),"instanceName":"1"}),"instanceName":"1"}),"instanceName":"1"}),"instanceName":"1"}),"instanceName":"1"}),"instanceName":"1"});
            var Q1290;
            Q1290=makeQuery(id+"F12.opPattern","COPY",BODY,{"derivedFrom":makeQuery(id+"F11.opPattern","COPY",BODY,{"derivedFrom":makeQuery(id+"F9.opPattern","COPY",BODY,{"derivedFrom":makeQuery(id+"F7.opPattern","COPY",BODY,{"derivedFrom":makeQuery(id+"F6.opPattern","COPY",BODY,{"derivedFrom":makeQuery(id+"F5.opPattern","COPY",BODY,{"derivedFrom":makeQuery(id+"F1.opRevolve","SWEPT_BODY",BODY,{"disambiguationData":[OSD([sQuery(id+"F0.wireOp",EDGE,"E1")])]}),"instanceName":"1"}),"instanceName":"1"}),"instanceName":"1"}),"instanceName":"1"}),"instanceName":"1"}),"instanceName":"1"});
            var Q1291;
            Q1291=makeQuery(id+"F12.opPattern","COPY",BODY,{"derivedFrom":makeQuery(id+"F11.opPattern","COPY",BODY,{"derivedFrom":makeQuery(id+"F9.opPattern","COPY",BODY,{"derivedFrom":makeQuery(id+"F7.opPattern","COPY",BODY,{"derivedFrom":makeQuery(id+"F6.opPattern","COPY",BODY,{"derivedFrom":makeQuery(id+"F5.opPattern","COPY",BODY,{"derivedFrom":makeQuery(id+"F2.opPattern","COPY",BODY,{"derivedFrom":makeQuery(id+"F1.opRevolve","SWEPT_BODY",BODY,{"disambiguationData":[OSD([sQuery(id+"F0.wireOp",EDGE,"E1")])]}),"instanceName":"1"}),"instanceName":"1"}),"instanceName":"1"}),"instanceName":"1"}),"instanceName":"1"}),"instanceName":"1"}),"instanceName":"1"});
            var Q1292;
            Q1292=makeQuery(id+"F12.opPattern","COPY",BODY,{"derivedFrom":makeQuery(id+"F11.opPattern","COPY",BODY,{"derivedFrom":makeQuery(id+"F9.opPattern","COPY",BODY,{"derivedFrom":makeQuery(id+"F7.opPattern","COPY",BODY,{"derivedFrom":makeQuery(id+"F6.opPattern","COPY",BODY,{"derivedFrom":makeQuery(id+"F5.opPattern","COPY",BODY,{"derivedFrom":makeQuery(id+"F3.opPattern","COPY",BODY,{"derivedFrom":makeQuery(id+"F2.opPattern","COPY",BODY,{"derivedFrom":makeQuery(id+"F1.opRevolve","SWEPT_BODY",BODY,{"disambiguationData":[OSD([sQuery(id+"F0.wireOp",EDGE,"E1")])]}),"instanceName":"1"}),"instanceName":"1"}),"instanceName":"1"}),"instanceName":"1"}),"instanceName":"1"}),"instanceName":"1"}),"instanceName":"1"}),"instanceName":"1"});
            var Q1293;
            Q1293=makeQuery(id+"F12.opPattern","COPY",BODY,{"derivedFrom":makeQuery(id+"F11.opPattern","COPY",BODY,{"derivedFrom":makeQuery(id+"F9.opPattern","COPY",BODY,{"derivedFrom":makeQuery(id+"F7.opPattern","COPY",BODY,{"derivedFrom":makeQuery(id+"F6.opPattern","COPY",BODY,{"derivedFrom":makeQuery(id+"F5.opPattern","COPY",BODY,{"derivedFrom":makeQuery(id+"F4.opPattern","COPY",BODY,{"derivedFrom":makeQuery(id+"F1.opRevolve","SWEPT_BODY",BODY,{"disambiguationData":[OSD([sQuery(id+"F0.wireOp",EDGE,"E1")])]}),"instanceName":"1"}),"instanceName":"1"}),"instanceName":"1"}),"instanceName":"1"}),"instanceName":"1"}),"instanceName":"1"}),"instanceName":"1"});
            var Q1294;
            Q1294=makeQuery(id+"F12.opPattern","COPY",BODY,{"derivedFrom":makeQuery(id+"F11.opPattern","COPY",BODY,{"derivedFrom":makeQuery(id+"F9.opPattern","COPY",BODY,{"derivedFrom":makeQuery(id+"F7.opPattern","COPY",BODY,{"derivedFrom":makeQuery(id+"F6.opPattern","COPY",BODY,{"derivedFrom":makeQuery(id+"F5.opPattern","COPY",BODY,{"derivedFrom":makeQuery(id+"F4.opPattern","COPY",BODY,{"derivedFrom":makeQuery(id+"F2.opPattern","COPY",BODY,{"derivedFrom":makeQuery(id+"F1.opRevolve","SWEPT_BODY",BODY,{"disambiguationData":[OSD([sQuery(id+"F0.wireOp",EDGE,"E1")])]}),"instanceName":"1"}),"instanceName":"1"}),"instanceName":"1"}),"instanceName":"1"}),"instanceName":"1"}),"instanceName":"1"}),"instanceName":"1"}),"instanceName":"1"});
            var Q1295;
            Q1295=makeQuery(id+"F12.opPattern","COPY",BODY,{"derivedFrom":makeQuery(id+"F11.opPattern","COPY",BODY,{"derivedFrom":makeQuery(id+"F9.opPattern","COPY",BODY,{"derivedFrom":makeQuery(id+"F7.opPattern","COPY",BODY,{"derivedFrom":makeQuery(id+"F6.opPattern","COPY",BODY,{"derivedFrom":makeQuery(id+"F5.opPattern","COPY",BODY,{"derivedFrom":makeQuery(id+"F4.opPattern","COPY",BODY,{"derivedFrom":makeQuery(id+"F3.opPattern","COPY",BODY,{"derivedFrom":makeQuery(id+"F2.opPattern","COPY",BODY,{"derivedFrom":makeQuery(id+"F1.opRevolve","SWEPT_BODY",BODY,{"disambiguationData":[OSD([sQuery(id+"F0.wireOp",EDGE,"E1")])]}),"instanceName":"1"}),"instanceName":"1"}),"instanceName":"1"}),"instanceName":"1"}),"instanceName":"1"}),"instanceName":"1"}),"instanceName":"1"}),"instanceName":"1"}),"instanceName":"1"});
            var Q1296;
            Q1296=makeQuery(id+"F12.opPattern","COPY",BODY,{"derivedFrom":makeQuery(id+"F11.opPattern","COPY",BODY,{"derivedFrom":makeQuery(id+"F9.opPattern","COPY",BODY,{"derivedFrom":makeQuery(id+"F8.opPattern","COPY",BODY,{"derivedFrom":makeQuery(id+"F1.opRevolve","SWEPT_BODY",BODY,{"disambiguationData":[OSD([sQuery(id+"F0.wireOp",EDGE,"E1")])]}),"instanceName":"1"}),"instanceName":"1"}),"instanceName":"1"}),"instanceName":"1"});
            var Q1297;
            Q1297=makeQuery(id+"F12.opPattern","COPY",BODY,{"derivedFrom":makeQuery(id+"F11.opPattern","COPY",BODY,{"derivedFrom":makeQuery(id+"F9.opPattern","COPY",BODY,{"derivedFrom":makeQuery(id+"F8.opPattern","COPY",BODY,{"derivedFrom":makeQuery(id+"F2.opPattern","COPY",BODY,{"derivedFrom":makeQuery(id+"F1.opRevolve","SWEPT_BODY",BODY,{"disambiguationData":[OSD([sQuery(id+"F0.wireOp",EDGE,"E1")])]}),"instanceName":"1"}),"instanceName":"1"}),"instanceName":"1"}),"instanceName":"1"}),"instanceName":"1"});
            var Q1298;
            Q1298=makeQuery(id+"F12.opPattern","COPY",BODY,{"derivedFrom":makeQuery(id+"F11.opPattern","COPY",BODY,{"derivedFrom":makeQuery(id+"F9.opPattern","COPY",BODY,{"derivedFrom":makeQuery(id+"F8.opPattern","COPY",BODY,{"derivedFrom":makeQuery(id+"F3.opPattern","COPY",BODY,{"derivedFrom":makeQuery(id+"F2.opPattern","COPY",BODY,{"derivedFrom":makeQuery(id+"F1.opRevolve","SWEPT_BODY",BODY,{"disambiguationData":[OSD([sQuery(id+"F0.wireOp",EDGE,"E1")])]}),"instanceName":"1"}),"instanceName":"1"}),"instanceName":"1"}),"instanceName":"1"}),"instanceName":"1"}),"instanceName":"1"});
            var Q1299;
            Q1299=makeQuery(id+"F12.opPattern","COPY",BODY,{"derivedFrom":makeQuery(id+"F11.opPattern","COPY",BODY,{"derivedFrom":makeQuery(id+"F9.opPattern","COPY",BODY,{"derivedFrom":makeQuery(id+"F8.opPattern","COPY",BODY,{"derivedFrom":makeQuery(id+"F4.opPattern","COPY",BODY,{"derivedFrom":makeQuery(id+"F1.opRevolve","SWEPT_BODY",BODY,{"disambiguationData":[OSD([sQuery(id+"F0.wireOp",EDGE,"E1")])]}),"instanceName":"1"}),"instanceName":"1"}),"instanceName":"1"}),"instanceName":"1"}),"instanceName":"1"});
            var Q1300;
            Q1300=makeQuery(id+"F12.opPattern","COPY",BODY,{"derivedFrom":makeQuery(id+"F11.opPattern","COPY",BODY,{"derivedFrom":makeQuery(id+"F9.opPattern","COPY",BODY,{"derivedFrom":makeQuery(id+"F8.opPattern","COPY",BODY,{"derivedFrom":makeQuery(id+"F4.opPattern","COPY",BODY,{"derivedFrom":makeQuery(id+"F2.opPattern","COPY",BODY,{"derivedFrom":makeQuery(id+"F1.opRevolve","SWEPT_BODY",BODY,{"disambiguationData":[OSD([sQuery(id+"F0.wireOp",EDGE,"E1")])]}),"instanceName":"1"}),"instanceName":"1"}),"instanceName":"1"}),"instanceName":"1"}),"instanceName":"1"}),"instanceName":"1"});
            var Q1301;
            Q1301=makeQuery(id+"F12.opPattern","COPY",BODY,{"derivedFrom":makeQuery(id+"F11.opPattern","COPY",BODY,{"derivedFrom":makeQuery(id+"F9.opPattern","COPY",BODY,{"derivedFrom":makeQuery(id+"F8.opPattern","COPY",BODY,{"derivedFrom":makeQuery(id+"F4.opPattern","COPY",BODY,{"derivedFrom":makeQuery(id+"F3.opPattern","COPY",BODY,{"derivedFrom":makeQuery(id+"F2.opPattern","COPY",BODY,{"derivedFrom":makeQuery(id+"F1.opRevolve","SWEPT_BODY",BODY,{"disambiguationData":[OSD([sQuery(id+"F0.wireOp",EDGE,"E1")])]}),"instanceName":"1"}),"instanceName":"1"}),"instanceName":"1"}),"instanceName":"1"}),"instanceName":"1"}),"instanceName":"1"}),"instanceName":"1"});
            var Q1302;
            Q1302=makeQuery(id+"F12.opPattern","COPY",BODY,{"derivedFrom":makeQuery(id+"F11.opPattern","COPY",BODY,{"derivedFrom":makeQuery(id+"F9.opPattern","COPY",BODY,{"derivedFrom":makeQuery(id+"F8.opPattern","COPY",BODY,{"derivedFrom":makeQuery(id+"F5.opPattern","COPY",BODY,{"derivedFrom":makeQuery(id+"F1.opRevolve","SWEPT_BODY",BODY,{"disambiguationData":[OSD([sQuery(id+"F0.wireOp",EDGE,"E1")])]}),"instanceName":"1"}),"instanceName":"1"}),"instanceName":"1"}),"instanceName":"1"}),"instanceName":"1"});
            var Q1303;
            Q1303=makeQuery(id+"F12.opPattern","COPY",BODY,{"derivedFrom":makeQuery(id+"F11.opPattern","COPY",BODY,{"derivedFrom":makeQuery(id+"F9.opPattern","COPY",BODY,{"derivedFrom":makeQuery(id+"F8.opPattern","COPY",BODY,{"derivedFrom":makeQuery(id+"F5.opPattern","COPY",BODY,{"derivedFrom":makeQuery(id+"F2.opPattern","COPY",BODY,{"derivedFrom":makeQuery(id+"F1.opRevolve","SWEPT_BODY",BODY,{"disambiguationData":[OSD([sQuery(id+"F0.wireOp",EDGE,"E1")])]}),"instanceName":"1"}),"instanceName":"1"}),"instanceName":"1"}),"instanceName":"1"}),"instanceName":"1"}),"instanceName":"1"});
            var Q1304;
            Q1304=makeQuery(id+"F12.opPattern","COPY",BODY,{"derivedFrom":makeQuery(id+"F11.opPattern","COPY",BODY,{"derivedFrom":makeQuery(id+"F9.opPattern","COPY",BODY,{"derivedFrom":makeQuery(id+"F8.opPattern","COPY",BODY,{"derivedFrom":makeQuery(id+"F5.opPattern","COPY",BODY,{"derivedFrom":makeQuery(id+"F3.opPattern","COPY",BODY,{"derivedFrom":makeQuery(id+"F2.opPattern","COPY",BODY,{"derivedFrom":makeQuery(id+"F1.opRevolve","SWEPT_BODY",BODY,{"disambiguationData":[OSD([sQuery(id+"F0.wireOp",EDGE,"E1")])]}),"instanceName":"1"}),"instanceName":"1"}),"instanceName":"1"}),"instanceName":"1"}),"instanceName":"1"}),"instanceName":"1"}),"instanceName":"1"});
            var Q1305;
            Q1305=makeQuery(id+"F12.opPattern","COPY",BODY,{"derivedFrom":makeQuery(id+"F11.opPattern","COPY",BODY,{"derivedFrom":makeQuery(id+"F9.opPattern","COPY",BODY,{"derivedFrom":makeQuery(id+"F8.opPattern","COPY",BODY,{"derivedFrom":makeQuery(id+"F5.opPattern","COPY",BODY,{"derivedFrom":makeQuery(id+"F4.opPattern","COPY",BODY,{"derivedFrom":makeQuery(id+"F1.opRevolve","SWEPT_BODY",BODY,{"disambiguationData":[OSD([sQuery(id+"F0.wireOp",EDGE,"E1")])]}),"instanceName":"1"}),"instanceName":"1"}),"instanceName":"1"}),"instanceName":"1"}),"instanceName":"1"}),"instanceName":"1"});
            var Q1306;
            Q1306=makeQuery(id+"F12.opPattern","COPY",BODY,{"derivedFrom":makeQuery(id+"F11.opPattern","COPY",BODY,{"derivedFrom":makeQuery(id+"F9.opPattern","COPY",BODY,{"derivedFrom":makeQuery(id+"F8.opPattern","COPY",BODY,{"derivedFrom":makeQuery(id+"F5.opPattern","COPY",BODY,{"derivedFrom":makeQuery(id+"F4.opPattern","COPY",BODY,{"derivedFrom":makeQuery(id+"F2.opPattern","COPY",BODY,{"derivedFrom":makeQuery(id+"F1.opRevolve","SWEPT_BODY",BODY,{"disambiguationData":[OSD([sQuery(id+"F0.wireOp",EDGE,"E1")])]}),"instanceName":"1"}),"instanceName":"1"}),"instanceName":"1"}),"instanceName":"1"}),"instanceName":"1"}),"instanceName":"1"}),"instanceName":"1"});
            var Q1307;
            Q1307=makeQuery(id+"F12.opPattern","COPY",BODY,{"derivedFrom":makeQuery(id+"F11.opPattern","COPY",BODY,{"derivedFrom":makeQuery(id+"F9.opPattern","COPY",BODY,{"derivedFrom":makeQuery(id+"F8.opPattern","COPY",BODY,{"derivedFrom":makeQuery(id+"F5.opPattern","COPY",BODY,{"derivedFrom":makeQuery(id+"F4.opPattern","COPY",BODY,{"derivedFrom":makeQuery(id+"F3.opPattern","COPY",BODY,{"derivedFrom":makeQuery(id+"F2.opPattern","COPY",BODY,{"derivedFrom":makeQuery(id+"F1.opRevolve","SWEPT_BODY",BODY,{"disambiguationData":[OSD([sQuery(id+"F0.wireOp",EDGE,"E1")])]}),"instanceName":"1"}),"instanceName":"1"}),"instanceName":"1"}),"instanceName":"1"}),"instanceName":"1"}),"instanceName":"1"}),"instanceName":"1"}),"instanceName":"1"});
            var Q1308;
            Q1308=makeQuery(id+"F12.opPattern","COPY",BODY,{"derivedFrom":makeQuery(id+"F11.opPattern","COPY",BODY,{"derivedFrom":makeQuery(id+"F9.opPattern","COPY",BODY,{"derivedFrom":makeQuery(id+"F8.opPattern","COPY",BODY,{"derivedFrom":makeQuery(id+"F6.opPattern","COPY",BODY,{"derivedFrom":makeQuery(id+"F1.opRevolve","SWEPT_BODY",BODY,{"disambiguationData":[OSD([sQuery(id+"F0.wireOp",EDGE,"E1")])]}),"instanceName":"1"}),"instanceName":"1"}),"instanceName":"1"}),"instanceName":"1"}),"instanceName":"1"});
            var Q1309;
            Q1309=makeQuery(id+"F12.opPattern","COPY",BODY,{"derivedFrom":makeQuery(id+"F11.opPattern","COPY",BODY,{"derivedFrom":makeQuery(id+"F9.opPattern","COPY",BODY,{"derivedFrom":makeQuery(id+"F8.opPattern","COPY",BODY,{"derivedFrom":makeQuery(id+"F6.opPattern","COPY",BODY,{"derivedFrom":makeQuery(id+"F2.opPattern","COPY",BODY,{"derivedFrom":makeQuery(id+"F1.opRevolve","SWEPT_BODY",BODY,{"disambiguationData":[OSD([sQuery(id+"F0.wireOp",EDGE,"E1")])]}),"instanceName":"1"}),"instanceName":"1"}),"instanceName":"1"}),"instanceName":"1"}),"instanceName":"1"}),"instanceName":"1"});
            var Q1310;
            Q1310=makeQuery(id+"F12.opPattern","COPY",BODY,{"derivedFrom":makeQuery(id+"F11.opPattern","COPY",BODY,{"derivedFrom":makeQuery(id+"F9.opPattern","COPY",BODY,{"derivedFrom":makeQuery(id+"F8.opPattern","COPY",BODY,{"derivedFrom":makeQuery(id+"F6.opPattern","COPY",BODY,{"derivedFrom":makeQuery(id+"F3.opPattern","COPY",BODY,{"derivedFrom":makeQuery(id+"F2.opPattern","COPY",BODY,{"derivedFrom":makeQuery(id+"F1.opRevolve","SWEPT_BODY",BODY,{"disambiguationData":[OSD([sQuery(id+"F0.wireOp",EDGE,"E1")])]}),"instanceName":"1"}),"instanceName":"1"}),"instanceName":"1"}),"instanceName":"1"}),"instanceName":"1"}),"instanceName":"1"}),"instanceName":"1"});
            var Q1311;
            Q1311=makeQuery(id+"F12.opPattern","COPY",BODY,{"derivedFrom":makeQuery(id+"F11.opPattern","COPY",BODY,{"derivedFrom":makeQuery(id+"F9.opPattern","COPY",BODY,{"derivedFrom":makeQuery(id+"F8.opPattern","COPY",BODY,{"derivedFrom":makeQuery(id+"F6.opPattern","COPY",BODY,{"derivedFrom":makeQuery(id+"F4.opPattern","COPY",BODY,{"derivedFrom":makeQuery(id+"F1.opRevolve","SWEPT_BODY",BODY,{"disambiguationData":[OSD([sQuery(id+"F0.wireOp",EDGE,"E1")])]}),"instanceName":"1"}),"instanceName":"1"}),"instanceName":"1"}),"instanceName":"1"}),"instanceName":"1"}),"instanceName":"1"});
            var Q1312;
            Q1312=makeQuery(id+"F12.opPattern","COPY",BODY,{"derivedFrom":makeQuery(id+"F11.opPattern","COPY",BODY,{"derivedFrom":makeQuery(id+"F9.opPattern","COPY",BODY,{"derivedFrom":makeQuery(id+"F8.opPattern","COPY",BODY,{"derivedFrom":makeQuery(id+"F6.opPattern","COPY",BODY,{"derivedFrom":makeQuery(id+"F4.opPattern","COPY",BODY,{"derivedFrom":makeQuery(id+"F2.opPattern","COPY",BODY,{"derivedFrom":makeQuery(id+"F1.opRevolve","SWEPT_BODY",BODY,{"disambiguationData":[OSD([sQuery(id+"F0.wireOp",EDGE,"E1")])]}),"instanceName":"1"}),"instanceName":"1"}),"instanceName":"1"}),"instanceName":"1"}),"instanceName":"1"}),"instanceName":"1"}),"instanceName":"1"});
            var Q1313;
            Q1313=makeQuery(id+"F12.opPattern","COPY",BODY,{"derivedFrom":makeQuery(id+"F11.opPattern","COPY",BODY,{"derivedFrom":makeQuery(id+"F9.opPattern","COPY",BODY,{"derivedFrom":makeQuery(id+"F8.opPattern","COPY",BODY,{"derivedFrom":makeQuery(id+"F6.opPattern","COPY",BODY,{"derivedFrom":makeQuery(id+"F4.opPattern","COPY",BODY,{"derivedFrom":makeQuery(id+"F3.opPattern","COPY",BODY,{"derivedFrom":makeQuery(id+"F2.opPattern","COPY",BODY,{"derivedFrom":makeQuery(id+"F1.opRevolve","SWEPT_BODY",BODY,{"disambiguationData":[OSD([sQuery(id+"F0.wireOp",EDGE,"E1")])]}),"instanceName":"1"}),"instanceName":"1"}),"instanceName":"1"}),"instanceName":"1"}),"instanceName":"1"}),"instanceName":"1"}),"instanceName":"1"}),"instanceName":"1"});
            var Q1314;
            Q1314=makeQuery(id+"F12.opPattern","COPY",BODY,{"derivedFrom":makeQuery(id+"F11.opPattern","COPY",BODY,{"derivedFrom":makeQuery(id+"F9.opPattern","COPY",BODY,{"derivedFrom":makeQuery(id+"F8.opPattern","COPY",BODY,{"derivedFrom":makeQuery(id+"F6.opPattern","COPY",BODY,{"derivedFrom":makeQuery(id+"F5.opPattern","COPY",BODY,{"derivedFrom":makeQuery(id+"F1.opRevolve","SWEPT_BODY",BODY,{"disambiguationData":[OSD([sQuery(id+"F0.wireOp",EDGE,"E1")])]}),"instanceName":"1"}),"instanceName":"1"}),"instanceName":"1"}),"instanceName":"1"}),"instanceName":"1"}),"instanceName":"1"});
            var Q1315;
            Q1315=makeQuery(id+"F12.opPattern","COPY",BODY,{"derivedFrom":makeQuery(id+"F11.opPattern","COPY",BODY,{"derivedFrom":makeQuery(id+"F9.opPattern","COPY",BODY,{"derivedFrom":makeQuery(id+"F8.opPattern","COPY",BODY,{"derivedFrom":makeQuery(id+"F6.opPattern","COPY",BODY,{"derivedFrom":makeQuery(id+"F5.opPattern","COPY",BODY,{"derivedFrom":makeQuery(id+"F2.opPattern","COPY",BODY,{"derivedFrom":makeQuery(id+"F1.opRevolve","SWEPT_BODY",BODY,{"disambiguationData":[OSD([sQuery(id+"F0.wireOp",EDGE,"E1")])]}),"instanceName":"1"}),"instanceName":"1"}),"instanceName":"1"}),"instanceName":"1"}),"instanceName":"1"}),"instanceName":"1"}),"instanceName":"1"});
            var Q1316;
            Q1316=makeQuery(id+"F12.opPattern","COPY",BODY,{"derivedFrom":makeQuery(id+"F11.opPattern","COPY",BODY,{"derivedFrom":makeQuery(id+"F9.opPattern","COPY",BODY,{"derivedFrom":makeQuery(id+"F8.opPattern","COPY",BODY,{"derivedFrom":makeQuery(id+"F6.opPattern","COPY",BODY,{"derivedFrom":makeQuery(id+"F5.opPattern","COPY",BODY,{"derivedFrom":makeQuery(id+"F3.opPattern","COPY",BODY,{"derivedFrom":makeQuery(id+"F2.opPattern","COPY",BODY,{"derivedFrom":makeQuery(id+"F1.opRevolve","SWEPT_BODY",BODY,{"disambiguationData":[OSD([sQuery(id+"F0.wireOp",EDGE,"E1")])]}),"instanceName":"1"}),"instanceName":"1"}),"instanceName":"1"}),"instanceName":"1"}),"instanceName":"1"}),"instanceName":"1"}),"instanceName":"1"}),"instanceName":"1"});
            var Q1317;
            Q1317=makeQuery(id+"F12.opPattern","COPY",BODY,{"derivedFrom":makeQuery(id+"F11.opPattern","COPY",BODY,{"derivedFrom":makeQuery(id+"F9.opPattern","COPY",BODY,{"derivedFrom":makeQuery(id+"F8.opPattern","COPY",BODY,{"derivedFrom":makeQuery(id+"F6.opPattern","COPY",BODY,{"derivedFrom":makeQuery(id+"F5.opPattern","COPY",BODY,{"derivedFrom":makeQuery(id+"F4.opPattern","COPY",BODY,{"derivedFrom":makeQuery(id+"F1.opRevolve","SWEPT_BODY",BODY,{"disambiguationData":[OSD([sQuery(id+"F0.wireOp",EDGE,"E1")])]}),"instanceName":"1"}),"instanceName":"1"}),"instanceName":"1"}),"instanceName":"1"}),"instanceName":"1"}),"instanceName":"1"}),"instanceName":"1"});
            var Q1318;
            Q1318=makeQuery(id+"F12.opPattern","COPY",BODY,{"derivedFrom":makeQuery(id+"F11.opPattern","COPY",BODY,{"derivedFrom":makeQuery(id+"F9.opPattern","COPY",BODY,{"derivedFrom":makeQuery(id+"F8.opPattern","COPY",BODY,{"derivedFrom":makeQuery(id+"F6.opPattern","COPY",BODY,{"derivedFrom":makeQuery(id+"F5.opPattern","COPY",BODY,{"derivedFrom":makeQuery(id+"F4.opPattern","COPY",BODY,{"derivedFrom":makeQuery(id+"F2.opPattern","COPY",BODY,{"derivedFrom":makeQuery(id+"F1.opRevolve","SWEPT_BODY",BODY,{"disambiguationData":[OSD([sQuery(id+"F0.wireOp",EDGE,"E1")])]}),"instanceName":"1"}),"instanceName":"1"}),"instanceName":"1"}),"instanceName":"1"}),"instanceName":"1"}),"instanceName":"1"}),"instanceName":"1"}),"instanceName":"1"});
            var Q1319;
            Q1319=makeQuery(id+"F12.opPattern","COPY",BODY,{"derivedFrom":makeQuery(id+"F11.opPattern","COPY",BODY,{"derivedFrom":makeQuery(id+"F9.opPattern","COPY",BODY,{"derivedFrom":makeQuery(id+"F8.opPattern","COPY",BODY,{"derivedFrom":makeQuery(id+"F6.opPattern","COPY",BODY,{"derivedFrom":makeQuery(id+"F5.opPattern","COPY",BODY,{"derivedFrom":makeQuery(id+"F4.opPattern","COPY",BODY,{"derivedFrom":makeQuery(id+"F3.opPattern","COPY",BODY,{"derivedFrom":makeQuery(id+"F2.opPattern","COPY",BODY,{"derivedFrom":makeQuery(id+"F1.opRevolve","SWEPT_BODY",BODY,{"disambiguationData":[OSD([sQuery(id+"F0.wireOp",EDGE,"E1")])]}),"instanceName":"1"}),"instanceName":"1"}),"instanceName":"1"}),"instanceName":"1"}),"instanceName":"1"}),"instanceName":"1"}),"instanceName":"1"}),"instanceName":"1"}),"instanceName":"1"});
            var Q1320;
            Q1320=makeQuery(id+"F12.opPattern","COPY",BODY,{"derivedFrom":makeQuery(id+"F11.opPattern","COPY",BODY,{"derivedFrom":makeQuery(id+"F9.opPattern","COPY",BODY,{"derivedFrom":makeQuery(id+"F8.opPattern","COPY",BODY,{"derivedFrom":makeQuery(id+"F7.opPattern","COPY",BODY,{"derivedFrom":makeQuery(id+"F1.opRevolve","SWEPT_BODY",BODY,{"disambiguationData":[OSD([sQuery(id+"F0.wireOp",EDGE,"E1")])]}),"instanceName":"1"}),"instanceName":"1"}),"instanceName":"1"}),"instanceName":"1"}),"instanceName":"1"});
            var Q1321;
            Q1321=makeQuery(id+"F12.opPattern","COPY",BODY,{"derivedFrom":makeQuery(id+"F11.opPattern","COPY",BODY,{"derivedFrom":makeQuery(id+"F9.opPattern","COPY",BODY,{"derivedFrom":makeQuery(id+"F8.opPattern","COPY",BODY,{"derivedFrom":makeQuery(id+"F7.opPattern","COPY",BODY,{"derivedFrom":makeQuery(id+"F2.opPattern","COPY",BODY,{"derivedFrom":makeQuery(id+"F1.opRevolve","SWEPT_BODY",BODY,{"disambiguationData":[OSD([sQuery(id+"F0.wireOp",EDGE,"E1")])]}),"instanceName":"1"}),"instanceName":"1"}),"instanceName":"1"}),"instanceName":"1"}),"instanceName":"1"}),"instanceName":"1"});
            var Q1322;
            Q1322=makeQuery(id+"F12.opPattern","COPY",BODY,{"derivedFrom":makeQuery(id+"F11.opPattern","COPY",BODY,{"derivedFrom":makeQuery(id+"F9.opPattern","COPY",BODY,{"derivedFrom":makeQuery(id+"F8.opPattern","COPY",BODY,{"derivedFrom":makeQuery(id+"F7.opPattern","COPY",BODY,{"derivedFrom":makeQuery(id+"F3.opPattern","COPY",BODY,{"derivedFrom":makeQuery(id+"F2.opPattern","COPY",BODY,{"derivedFrom":makeQuery(id+"F1.opRevolve","SWEPT_BODY",BODY,{"disambiguationData":[OSD([sQuery(id+"F0.wireOp",EDGE,"E1")])]}),"instanceName":"1"}),"instanceName":"1"}),"instanceName":"1"}),"instanceName":"1"}),"instanceName":"1"}),"instanceName":"1"}),"instanceName":"1"});
            var Q1323;
            Q1323=makeQuery(id+"F12.opPattern","COPY",BODY,{"derivedFrom":makeQuery(id+"F11.opPattern","COPY",BODY,{"derivedFrom":makeQuery(id+"F9.opPattern","COPY",BODY,{"derivedFrom":makeQuery(id+"F8.opPattern","COPY",BODY,{"derivedFrom":makeQuery(id+"F7.opPattern","COPY",BODY,{"derivedFrom":makeQuery(id+"F4.opPattern","COPY",BODY,{"derivedFrom":makeQuery(id+"F1.opRevolve","SWEPT_BODY",BODY,{"disambiguationData":[OSD([sQuery(id+"F0.wireOp",EDGE,"E1")])]}),"instanceName":"1"}),"instanceName":"1"}),"instanceName":"1"}),"instanceName":"1"}),"instanceName":"1"}),"instanceName":"1"});
            var Q1324;
            Q1324=makeQuery(id+"F12.opPattern","COPY",BODY,{"derivedFrom":makeQuery(id+"F11.opPattern","COPY",BODY,{"derivedFrom":makeQuery(id+"F9.opPattern","COPY",BODY,{"derivedFrom":makeQuery(id+"F8.opPattern","COPY",BODY,{"derivedFrom":makeQuery(id+"F7.opPattern","COPY",BODY,{"derivedFrom":makeQuery(id+"F4.opPattern","COPY",BODY,{"derivedFrom":makeQuery(id+"F2.opPattern","COPY",BODY,{"derivedFrom":makeQuery(id+"F1.opRevolve","SWEPT_BODY",BODY,{"disambiguationData":[OSD([sQuery(id+"F0.wireOp",EDGE,"E1")])]}),"instanceName":"1"}),"instanceName":"1"}),"instanceName":"1"}),"instanceName":"1"}),"instanceName":"1"}),"instanceName":"1"}),"instanceName":"1"});
            var Q1325;
            Q1325=makeQuery(id+"F12.opPattern","COPY",BODY,{"derivedFrom":makeQuery(id+"F11.opPattern","COPY",BODY,{"derivedFrom":makeQuery(id+"F9.opPattern","COPY",BODY,{"derivedFrom":makeQuery(id+"F8.opPattern","COPY",BODY,{"derivedFrom":makeQuery(id+"F7.opPattern","COPY",BODY,{"derivedFrom":makeQuery(id+"F4.opPattern","COPY",BODY,{"derivedFrom":makeQuery(id+"F3.opPattern","COPY",BODY,{"derivedFrom":makeQuery(id+"F2.opPattern","COPY",BODY,{"derivedFrom":makeQuery(id+"F1.opRevolve","SWEPT_BODY",BODY,{"disambiguationData":[OSD([sQuery(id+"F0.wireOp",EDGE,"E1")])]}),"instanceName":"1"}),"instanceName":"1"}),"instanceName":"1"}),"instanceName":"1"}),"instanceName":"1"}),"instanceName":"1"}),"instanceName":"1"}),"instanceName":"1"});
            var Q1326;
            Q1326=makeQuery(id+"F12.opPattern","COPY",BODY,{"derivedFrom":makeQuery(id+"F11.opPattern","COPY",BODY,{"derivedFrom":makeQuery(id+"F9.opPattern","COPY",BODY,{"derivedFrom":makeQuery(id+"F8.opPattern","COPY",BODY,{"derivedFrom":makeQuery(id+"F7.opPattern","COPY",BODY,{"derivedFrom":makeQuery(id+"F5.opPattern","COPY",BODY,{"derivedFrom":makeQuery(id+"F1.opRevolve","SWEPT_BODY",BODY,{"disambiguationData":[OSD([sQuery(id+"F0.wireOp",EDGE,"E1")])]}),"instanceName":"1"}),"instanceName":"1"}),"instanceName":"1"}),"instanceName":"1"}),"instanceName":"1"}),"instanceName":"1"});
            var Q1327;
            Q1327=makeQuery(id+"F12.opPattern","COPY",BODY,{"derivedFrom":makeQuery(id+"F11.opPattern","COPY",BODY,{"derivedFrom":makeQuery(id+"F9.opPattern","COPY",BODY,{"derivedFrom":makeQuery(id+"F8.opPattern","COPY",BODY,{"derivedFrom":makeQuery(id+"F7.opPattern","COPY",BODY,{"derivedFrom":makeQuery(id+"F5.opPattern","COPY",BODY,{"derivedFrom":makeQuery(id+"F2.opPattern","COPY",BODY,{"derivedFrom":makeQuery(id+"F1.opRevolve","SWEPT_BODY",BODY,{"disambiguationData":[OSD([sQuery(id+"F0.wireOp",EDGE,"E1")])]}),"instanceName":"1"}),"instanceName":"1"}),"instanceName":"1"}),"instanceName":"1"}),"instanceName":"1"}),"instanceName":"1"}),"instanceName":"1"});
            var Q1328;
            Q1328=makeQuery(id+"F12.opPattern","COPY",BODY,{"derivedFrom":makeQuery(id+"F11.opPattern","COPY",BODY,{"derivedFrom":makeQuery(id+"F9.opPattern","COPY",BODY,{"derivedFrom":makeQuery(id+"F8.opPattern","COPY",BODY,{"derivedFrom":makeQuery(id+"F7.opPattern","COPY",BODY,{"derivedFrom":makeQuery(id+"F5.opPattern","COPY",BODY,{"derivedFrom":makeQuery(id+"F3.opPattern","COPY",BODY,{"derivedFrom":makeQuery(id+"F2.opPattern","COPY",BODY,{"derivedFrom":makeQuery(id+"F1.opRevolve","SWEPT_BODY",BODY,{"disambiguationData":[OSD([sQuery(id+"F0.wireOp",EDGE,"E1")])]}),"instanceName":"1"}),"instanceName":"1"}),"instanceName":"1"}),"instanceName":"1"}),"instanceName":"1"}),"instanceName":"1"}),"instanceName":"1"}),"instanceName":"1"});
            var Q1329;
            Q1329=makeQuery(id+"F12.opPattern","COPY",BODY,{"derivedFrom":makeQuery(id+"F11.opPattern","COPY",BODY,{"derivedFrom":makeQuery(id+"F9.opPattern","COPY",BODY,{"derivedFrom":makeQuery(id+"F8.opPattern","COPY",BODY,{"derivedFrom":makeQuery(id+"F7.opPattern","COPY",BODY,{"derivedFrom":makeQuery(id+"F5.opPattern","COPY",BODY,{"derivedFrom":makeQuery(id+"F4.opPattern","COPY",BODY,{"derivedFrom":makeQuery(id+"F1.opRevolve","SWEPT_BODY",BODY,{"disambiguationData":[OSD([sQuery(id+"F0.wireOp",EDGE,"E1")])]}),"instanceName":"1"}),"instanceName":"1"}),"instanceName":"1"}),"instanceName":"1"}),"instanceName":"1"}),"instanceName":"1"}),"instanceName":"1"});
            var Q1330;
            Q1330=makeQuery(id+"F12.opPattern","COPY",BODY,{"derivedFrom":makeQuery(id+"F11.opPattern","COPY",BODY,{"derivedFrom":makeQuery(id+"F9.opPattern","COPY",BODY,{"derivedFrom":makeQuery(id+"F8.opPattern","COPY",BODY,{"derivedFrom":makeQuery(id+"F7.opPattern","COPY",BODY,{"derivedFrom":makeQuery(id+"F5.opPattern","COPY",BODY,{"derivedFrom":makeQuery(id+"F4.opPattern","COPY",BODY,{"derivedFrom":makeQuery(id+"F2.opPattern","COPY",BODY,{"derivedFrom":makeQuery(id+"F1.opRevolve","SWEPT_BODY",BODY,{"disambiguationData":[OSD([sQuery(id+"F0.wireOp",EDGE,"E1")])]}),"instanceName":"1"}),"instanceName":"1"}),"instanceName":"1"}),"instanceName":"1"}),"instanceName":"1"}),"instanceName":"1"}),"instanceName":"1"}),"instanceName":"1"});
            var Q1331;
            Q1331=makeQuery(id+"F12.opPattern","COPY",BODY,{"derivedFrom":makeQuery(id+"F11.opPattern","COPY",BODY,{"derivedFrom":makeQuery(id+"F9.opPattern","COPY",BODY,{"derivedFrom":makeQuery(id+"F8.opPattern","COPY",BODY,{"derivedFrom":makeQuery(id+"F7.opPattern","COPY",BODY,{"derivedFrom":makeQuery(id+"F5.opPattern","COPY",BODY,{"derivedFrom":makeQuery(id+"F4.opPattern","COPY",BODY,{"derivedFrom":makeQuery(id+"F3.opPattern","COPY",BODY,{"derivedFrom":makeQuery(id+"F2.opPattern","COPY",BODY,{"derivedFrom":makeQuery(id+"F1.opRevolve","SWEPT_BODY",BODY,{"disambiguationData":[OSD([sQuery(id+"F0.wireOp",EDGE,"E1")])]}),"instanceName":"1"}),"instanceName":"1"}),"instanceName":"1"}),"instanceName":"1"}),"instanceName":"1"}),"instanceName":"1"}),"instanceName":"1"}),"instanceName":"1"}),"instanceName":"1"});
            var Q1332;
            Q1332=makeQuery(id+"F12.opPattern","COPY",BODY,{"derivedFrom":makeQuery(id+"F11.opPattern","COPY",BODY,{"derivedFrom":makeQuery(id+"F9.opPattern","COPY",BODY,{"derivedFrom":makeQuery(id+"F8.opPattern","COPY",BODY,{"derivedFrom":makeQuery(id+"F7.opPattern","COPY",BODY,{"derivedFrom":makeQuery(id+"F6.opPattern","COPY",BODY,{"derivedFrom":makeQuery(id+"F1.opRevolve","SWEPT_BODY",BODY,{"disambiguationData":[OSD([sQuery(id+"F0.wireOp",EDGE,"E1")])]}),"instanceName":"1"}),"instanceName":"1"}),"instanceName":"1"}),"instanceName":"1"}),"instanceName":"1"}),"instanceName":"1"});
            var Q1333;
            Q1333=makeQuery(id+"F12.opPattern","COPY",BODY,{"derivedFrom":makeQuery(id+"F11.opPattern","COPY",BODY,{"derivedFrom":makeQuery(id+"F9.opPattern","COPY",BODY,{"derivedFrom":makeQuery(id+"F8.opPattern","COPY",BODY,{"derivedFrom":makeQuery(id+"F7.opPattern","COPY",BODY,{"derivedFrom":makeQuery(id+"F6.opPattern","COPY",BODY,{"derivedFrom":makeQuery(id+"F2.opPattern","COPY",BODY,{"derivedFrom":makeQuery(id+"F1.opRevolve","SWEPT_BODY",BODY,{"disambiguationData":[OSD([sQuery(id+"F0.wireOp",EDGE,"E1")])]}),"instanceName":"1"}),"instanceName":"1"}),"instanceName":"1"}),"instanceName":"1"}),"instanceName":"1"}),"instanceName":"1"}),"instanceName":"1"});
            var Q1334;
            Q1334=makeQuery(id+"F12.opPattern","COPY",BODY,{"derivedFrom":makeQuery(id+"F11.opPattern","COPY",BODY,{"derivedFrom":makeQuery(id+"F9.opPattern","COPY",BODY,{"derivedFrom":makeQuery(id+"F8.opPattern","COPY",BODY,{"derivedFrom":makeQuery(id+"F7.opPattern","COPY",BODY,{"derivedFrom":makeQuery(id+"F6.opPattern","COPY",BODY,{"derivedFrom":makeQuery(id+"F3.opPattern","COPY",BODY,{"derivedFrom":makeQuery(id+"F2.opPattern","COPY",BODY,{"derivedFrom":makeQuery(id+"F1.opRevolve","SWEPT_BODY",BODY,{"disambiguationData":[OSD([sQuery(id+"F0.wireOp",EDGE,"E1")])]}),"instanceName":"1"}),"instanceName":"1"}),"instanceName":"1"}),"instanceName":"1"}),"instanceName":"1"}),"instanceName":"1"}),"instanceName":"1"}),"instanceName":"1"});
            var Q1335;
            Q1335=makeQuery(id+"F12.opPattern","COPY",BODY,{"derivedFrom":makeQuery(id+"F11.opPattern","COPY",BODY,{"derivedFrom":makeQuery(id+"F9.opPattern","COPY",BODY,{"derivedFrom":makeQuery(id+"F8.opPattern","COPY",BODY,{"derivedFrom":makeQuery(id+"F7.opPattern","COPY",BODY,{"derivedFrom":makeQuery(id+"F6.opPattern","COPY",BODY,{"derivedFrom":makeQuery(id+"F4.opPattern","COPY",BODY,{"derivedFrom":makeQuery(id+"F1.opRevolve","SWEPT_BODY",BODY,{"disambiguationData":[OSD([sQuery(id+"F0.wireOp",EDGE,"E1")])]}),"instanceName":"1"}),"instanceName":"1"}),"instanceName":"1"}),"instanceName":"1"}),"instanceName":"1"}),"instanceName":"1"}),"instanceName":"1"});
            var Q1336;
            Q1336=makeQuery(id+"F12.opPattern","COPY",BODY,{"derivedFrom":makeQuery(id+"F11.opPattern","COPY",BODY,{"derivedFrom":makeQuery(id+"F9.opPattern","COPY",BODY,{"derivedFrom":makeQuery(id+"F8.opPattern","COPY",BODY,{"derivedFrom":makeQuery(id+"F7.opPattern","COPY",BODY,{"derivedFrom":makeQuery(id+"F6.opPattern","COPY",BODY,{"derivedFrom":makeQuery(id+"F4.opPattern","COPY",BODY,{"derivedFrom":makeQuery(id+"F2.opPattern","COPY",BODY,{"derivedFrom":makeQuery(id+"F1.opRevolve","SWEPT_BODY",BODY,{"disambiguationData":[OSD([sQuery(id+"F0.wireOp",EDGE,"E1")])]}),"instanceName":"1"}),"instanceName":"1"}),"instanceName":"1"}),"instanceName":"1"}),"instanceName":"1"}),"instanceName":"1"}),"instanceName":"1"}),"instanceName":"1"});
            var Q1337;
            Q1337=makeQuery(id+"F12.opPattern","COPY",BODY,{"derivedFrom":makeQuery(id+"F11.opPattern","COPY",BODY,{"derivedFrom":makeQuery(id+"F9.opPattern","COPY",BODY,{"derivedFrom":makeQuery(id+"F8.opPattern","COPY",BODY,{"derivedFrom":makeQuery(id+"F7.opPattern","COPY",BODY,{"derivedFrom":makeQuery(id+"F6.opPattern","COPY",BODY,{"derivedFrom":makeQuery(id+"F4.opPattern","COPY",BODY,{"derivedFrom":makeQuery(id+"F3.opPattern","COPY",BODY,{"derivedFrom":makeQuery(id+"F2.opPattern","COPY",BODY,{"derivedFrom":makeQuery(id+"F1.opRevolve","SWEPT_BODY",BODY,{"disambiguationData":[OSD([sQuery(id+"F0.wireOp",EDGE,"E1")])]}),"instanceName":"1"}),"instanceName":"1"}),"instanceName":"1"}),"instanceName":"1"}),"instanceName":"1"}),"instanceName":"1"}),"instanceName":"1"}),"instanceName":"1"}),"instanceName":"1"});
            var Q1338;
            Q1338=makeQuery(id+"F12.opPattern","COPY",BODY,{"derivedFrom":makeQuery(id+"F11.opPattern","COPY",BODY,{"derivedFrom":makeQuery(id+"F9.opPattern","COPY",BODY,{"derivedFrom":makeQuery(id+"F8.opPattern","COPY",BODY,{"derivedFrom":makeQuery(id+"F7.opPattern","COPY",BODY,{"derivedFrom":makeQuery(id+"F6.opPattern","COPY",BODY,{"derivedFrom":makeQuery(id+"F5.opPattern","COPY",BODY,{"derivedFrom":makeQuery(id+"F1.opRevolve","SWEPT_BODY",BODY,{"disambiguationData":[OSD([sQuery(id+"F0.wireOp",EDGE,"E1")])]}),"instanceName":"1"}),"instanceName":"1"}),"instanceName":"1"}),"instanceName":"1"}),"instanceName":"1"}),"instanceName":"1"}),"instanceName":"1"});
            var Q1339;
            Q1339=makeQuery(id+"F12.opPattern","COPY",BODY,{"derivedFrom":makeQuery(id+"F11.opPattern","COPY",BODY,{"derivedFrom":makeQuery(id+"F9.opPattern","COPY",BODY,{"derivedFrom":makeQuery(id+"F8.opPattern","COPY",BODY,{"derivedFrom":makeQuery(id+"F7.opPattern","COPY",BODY,{"derivedFrom":makeQuery(id+"F6.opPattern","COPY",BODY,{"derivedFrom":makeQuery(id+"F5.opPattern","COPY",BODY,{"derivedFrom":makeQuery(id+"F2.opPattern","COPY",BODY,{"derivedFrom":makeQuery(id+"F1.opRevolve","SWEPT_BODY",BODY,{"disambiguationData":[OSD([sQuery(id+"F0.wireOp",EDGE,"E1")])]}),"instanceName":"1"}),"instanceName":"1"}),"instanceName":"1"}),"instanceName":"1"}),"instanceName":"1"}),"instanceName":"1"}),"instanceName":"1"}),"instanceName":"1"});
            var Q1340;
            Q1340=makeQuery(id+"F12.opPattern","COPY",BODY,{"derivedFrom":makeQuery(id+"F11.opPattern","COPY",BODY,{"derivedFrom":makeQuery(id+"F9.opPattern","COPY",BODY,{"derivedFrom":makeQuery(id+"F8.opPattern","COPY",BODY,{"derivedFrom":makeQuery(id+"F7.opPattern","COPY",BODY,{"derivedFrom":makeQuery(id+"F6.opPattern","COPY",BODY,{"derivedFrom":makeQuery(id+"F5.opPattern","COPY",BODY,{"derivedFrom":makeQuery(id+"F3.opPattern","COPY",BODY,{"derivedFrom":makeQuery(id+"F2.opPattern","COPY",BODY,{"derivedFrom":makeQuery(id+"F1.opRevolve","SWEPT_BODY",BODY,{"disambiguationData":[OSD([sQuery(id+"F0.wireOp",EDGE,"E1")])]}),"instanceName":"1"}),"instanceName":"1"}),"instanceName":"1"}),"instanceName":"1"}),"instanceName":"1"}),"instanceName":"1"}),"instanceName":"1"}),"instanceName":"1"}),"instanceName":"1"});
            var Q1341;
            Q1341=makeQuery(id+"F12.opPattern","COPY",BODY,{"derivedFrom":makeQuery(id+"F11.opPattern","COPY",BODY,{"derivedFrom":makeQuery(id+"F9.opPattern","COPY",BODY,{"derivedFrom":makeQuery(id+"F8.opPattern","COPY",BODY,{"derivedFrom":makeQuery(id+"F7.opPattern","COPY",BODY,{"derivedFrom":makeQuery(id+"F6.opPattern","COPY",BODY,{"derivedFrom":makeQuery(id+"F5.opPattern","COPY",BODY,{"derivedFrom":makeQuery(id+"F4.opPattern","COPY",BODY,{"derivedFrom":makeQuery(id+"F1.opRevolve","SWEPT_BODY",BODY,{"disambiguationData":[OSD([sQuery(id+"F0.wireOp",EDGE,"E1")])]}),"instanceName":"1"}),"instanceName":"1"}),"instanceName":"1"}),"instanceName":"1"}),"instanceName":"1"}),"instanceName":"1"}),"instanceName":"1"}),"instanceName":"1"});
            var Q1342;
            Q1342=makeQuery(id+"F12.opPattern","COPY",BODY,{"derivedFrom":makeQuery(id+"F11.opPattern","COPY",BODY,{"derivedFrom":makeQuery(id+"F9.opPattern","COPY",BODY,{"derivedFrom":makeQuery(id+"F8.opPattern","COPY",BODY,{"derivedFrom":makeQuery(id+"F7.opPattern","COPY",BODY,{"derivedFrom":makeQuery(id+"F6.opPattern","COPY",BODY,{"derivedFrom":makeQuery(id+"F5.opPattern","COPY",BODY,{"derivedFrom":makeQuery(id+"F4.opPattern","COPY",BODY,{"derivedFrom":makeQuery(id+"F2.opPattern","COPY",BODY,{"derivedFrom":makeQuery(id+"F1.opRevolve","SWEPT_BODY",BODY,{"disambiguationData":[OSD([sQuery(id+"F0.wireOp",EDGE,"E1")])]}),"instanceName":"1"}),"instanceName":"1"}),"instanceName":"1"}),"instanceName":"1"}),"instanceName":"1"}),"instanceName":"1"}),"instanceName":"1"}),"instanceName":"1"}),"instanceName":"1"});
            var Q1343;
            Q1343=makeQuery(id+"F12.opPattern","COPY",BODY,{"derivedFrom":makeQuery(id+"F11.opPattern","COPY",BODY,{"derivedFrom":makeQuery(id+"F9.opPattern","COPY",BODY,{"derivedFrom":makeQuery(id+"F8.opPattern","COPY",BODY,{"derivedFrom":makeQuery(id+"F7.opPattern","COPY",BODY,{"derivedFrom":makeQuery(id+"F6.opPattern","COPY",BODY,{"derivedFrom":makeQuery(id+"F5.opPattern","COPY",BODY,{"derivedFrom":makeQuery(id+"F4.opPattern","COPY",BODY,{"derivedFrom":makeQuery(id+"F3.opPattern","COPY",BODY,{"derivedFrom":makeQuery(id+"F2.opPattern","COPY",BODY,{"derivedFrom":makeQuery(id+"F1.opRevolve","SWEPT_BODY",BODY,{"disambiguationData":[OSD([sQuery(id+"F0.wireOp",EDGE,"E1")])]}),"instanceName":"1"}),"instanceName":"1"}),"instanceName":"1"}),"instanceName":"1"}),"instanceName":"1"}),"instanceName":"1"}),"instanceName":"1"}),"instanceName":"1"}),"instanceName":"1"}),"instanceName":"1"});
            var Q1344;
            Q1344=makeQuery(id+"F12.opPattern","COPY",BODY,{"derivedFrom":makeQuery(id+"F11.opPattern","COPY",BODY,{"derivedFrom":makeQuery(id+"F10.opPattern","COPY",BODY,{"derivedFrom":makeQuery(id+"F1.opRevolve","SWEPT_BODY",BODY,{"disambiguationData":[OSD([sQuery(id+"F0.wireOp",EDGE,"E1")])]}),"instanceName":"1"}),"instanceName":"1"}),"instanceName":"1"});
            var Q1345;
            Q1345=makeQuery(id+"F12.opPattern","COPY",BODY,{"derivedFrom":makeQuery(id+"F11.opPattern","COPY",BODY,{"derivedFrom":makeQuery(id+"F10.opPattern","COPY",BODY,{"derivedFrom":makeQuery(id+"F2.opPattern","COPY",BODY,{"derivedFrom":makeQuery(id+"F1.opRevolve","SWEPT_BODY",BODY,{"disambiguationData":[OSD([sQuery(id+"F0.wireOp",EDGE,"E1")])]}),"instanceName":"1"}),"instanceName":"1"}),"instanceName":"1"}),"instanceName":"1"});
            var Q1346;
            Q1346=makeQuery(id+"F12.opPattern","COPY",BODY,{"derivedFrom":makeQuery(id+"F11.opPattern","COPY",BODY,{"derivedFrom":makeQuery(id+"F10.opPattern","COPY",BODY,{"derivedFrom":makeQuery(id+"F3.opPattern","COPY",BODY,{"derivedFrom":makeQuery(id+"F2.opPattern","COPY",BODY,{"derivedFrom":makeQuery(id+"F1.opRevolve","SWEPT_BODY",BODY,{"disambiguationData":[OSD([sQuery(id+"F0.wireOp",EDGE,"E1")])]}),"instanceName":"1"}),"instanceName":"1"}),"instanceName":"1"}),"instanceName":"1"}),"instanceName":"1"});
            var Q1347;
            Q1347=makeQuery(id+"F12.opPattern","COPY",BODY,{"derivedFrom":makeQuery(id+"F11.opPattern","COPY",BODY,{"derivedFrom":makeQuery(id+"F10.opPattern","COPY",BODY,{"derivedFrom":makeQuery(id+"F4.opPattern","COPY",BODY,{"derivedFrom":makeQuery(id+"F1.opRevolve","SWEPT_BODY",BODY,{"disambiguationData":[OSD([sQuery(id+"F0.wireOp",EDGE,"E1")])]}),"instanceName":"1"}),"instanceName":"1"}),"instanceName":"1"}),"instanceName":"1"});
            var Q1348;
            Q1348=makeQuery(id+"F12.opPattern","COPY",BODY,{"derivedFrom":makeQuery(id+"F11.opPattern","COPY",BODY,{"derivedFrom":makeQuery(id+"F10.opPattern","COPY",BODY,{"derivedFrom":makeQuery(id+"F4.opPattern","COPY",BODY,{"derivedFrom":makeQuery(id+"F2.opPattern","COPY",BODY,{"derivedFrom":makeQuery(id+"F1.opRevolve","SWEPT_BODY",BODY,{"disambiguationData":[OSD([sQuery(id+"F0.wireOp",EDGE,"E1")])]}),"instanceName":"1"}),"instanceName":"1"}),"instanceName":"1"}),"instanceName":"1"}),"instanceName":"1"});
            var Q1349;
            Q1349=makeQuery(id+"F12.opPattern","COPY",BODY,{"derivedFrom":makeQuery(id+"F11.opPattern","COPY",BODY,{"derivedFrom":makeQuery(id+"F10.opPattern","COPY",BODY,{"derivedFrom":makeQuery(id+"F4.opPattern","COPY",BODY,{"derivedFrom":makeQuery(id+"F3.opPattern","COPY",BODY,{"derivedFrom":makeQuery(id+"F2.opPattern","COPY",BODY,{"derivedFrom":makeQuery(id+"F1.opRevolve","SWEPT_BODY",BODY,{"disambiguationData":[OSD([sQuery(id+"F0.wireOp",EDGE,"E1")])]}),"instanceName":"1"}),"instanceName":"1"}),"instanceName":"1"}),"instanceName":"1"}),"instanceName":"1"}),"instanceName":"1"});
            var Q1350;
            Q1350=makeQuery(id+"F12.opPattern","COPY",BODY,{"derivedFrom":makeQuery(id+"F11.opPattern","COPY",BODY,{"derivedFrom":makeQuery(id+"F10.opPattern","COPY",BODY,{"derivedFrom":makeQuery(id+"F5.opPattern","COPY",BODY,{"derivedFrom":makeQuery(id+"F1.opRevolve","SWEPT_BODY",BODY,{"disambiguationData":[OSD([sQuery(id+"F0.wireOp",EDGE,"E1")])]}),"instanceName":"1"}),"instanceName":"1"}),"instanceName":"1"}),"instanceName":"1"});
            var Q1351;
            Q1351=makeQuery(id+"F12.opPattern","COPY",BODY,{"derivedFrom":makeQuery(id+"F11.opPattern","COPY",BODY,{"derivedFrom":makeQuery(id+"F10.opPattern","COPY",BODY,{"derivedFrom":makeQuery(id+"F5.opPattern","COPY",BODY,{"derivedFrom":makeQuery(id+"F2.opPattern","COPY",BODY,{"derivedFrom":makeQuery(id+"F1.opRevolve","SWEPT_BODY",BODY,{"disambiguationData":[OSD([sQuery(id+"F0.wireOp",EDGE,"E1")])]}),"instanceName":"1"}),"instanceName":"1"}),"instanceName":"1"}),"instanceName":"1"}),"instanceName":"1"});
            var Q1352;
            Q1352=makeQuery(id+"F12.opPattern","COPY",BODY,{"derivedFrom":makeQuery(id+"F11.opPattern","COPY",BODY,{"derivedFrom":makeQuery(id+"F10.opPattern","COPY",BODY,{"derivedFrom":makeQuery(id+"F5.opPattern","COPY",BODY,{"derivedFrom":makeQuery(id+"F3.opPattern","COPY",BODY,{"derivedFrom":makeQuery(id+"F2.opPattern","COPY",BODY,{"derivedFrom":makeQuery(id+"F1.opRevolve","SWEPT_BODY",BODY,{"disambiguationData":[OSD([sQuery(id+"F0.wireOp",EDGE,"E1")])]}),"instanceName":"1"}),"instanceName":"1"}),"instanceName":"1"}),"instanceName":"1"}),"instanceName":"1"}),"instanceName":"1"});
            var Q1353;
            Q1353=makeQuery(id+"F12.opPattern","COPY",BODY,{"derivedFrom":makeQuery(id+"F11.opPattern","COPY",BODY,{"derivedFrom":makeQuery(id+"F10.opPattern","COPY",BODY,{"derivedFrom":makeQuery(id+"F5.opPattern","COPY",BODY,{"derivedFrom":makeQuery(id+"F4.opPattern","COPY",BODY,{"derivedFrom":makeQuery(id+"F1.opRevolve","SWEPT_BODY",BODY,{"disambiguationData":[OSD([sQuery(id+"F0.wireOp",EDGE,"E1")])]}),"instanceName":"1"}),"instanceName":"1"}),"instanceName":"1"}),"instanceName":"1"}),"instanceName":"1"});
            var Q1354;
            Q1354=makeQuery(id+"F12.opPattern","COPY",BODY,{"derivedFrom":makeQuery(id+"F11.opPattern","COPY",BODY,{"derivedFrom":makeQuery(id+"F10.opPattern","COPY",BODY,{"derivedFrom":makeQuery(id+"F5.opPattern","COPY",BODY,{"derivedFrom":makeQuery(id+"F4.opPattern","COPY",BODY,{"derivedFrom":makeQuery(id+"F2.opPattern","COPY",BODY,{"derivedFrom":makeQuery(id+"F1.opRevolve","SWEPT_BODY",BODY,{"disambiguationData":[OSD([sQuery(id+"F0.wireOp",EDGE,"E1")])]}),"instanceName":"1"}),"instanceName":"1"}),"instanceName":"1"}),"instanceName":"1"}),"instanceName":"1"}),"instanceName":"1"});
            var Q1355;
            Q1355=makeQuery(id+"F12.opPattern","COPY",BODY,{"derivedFrom":makeQuery(id+"F11.opPattern","COPY",BODY,{"derivedFrom":makeQuery(id+"F10.opPattern","COPY",BODY,{"derivedFrom":makeQuery(id+"F5.opPattern","COPY",BODY,{"derivedFrom":makeQuery(id+"F4.opPattern","COPY",BODY,{"derivedFrom":makeQuery(id+"F3.opPattern","COPY",BODY,{"derivedFrom":makeQuery(id+"F2.opPattern","COPY",BODY,{"derivedFrom":makeQuery(id+"F1.opRevolve","SWEPT_BODY",BODY,{"disambiguationData":[OSD([sQuery(id+"F0.wireOp",EDGE,"E1")])]}),"instanceName":"1"}),"instanceName":"1"}),"instanceName":"1"}),"instanceName":"1"}),"instanceName":"1"}),"instanceName":"1"}),"instanceName":"1"});
            var Q1356;
            Q1356=makeQuery(id+"F12.opPattern","COPY",BODY,{"derivedFrom":makeQuery(id+"F11.opPattern","COPY",BODY,{"derivedFrom":makeQuery(id+"F10.opPattern","COPY",BODY,{"derivedFrom":makeQuery(id+"F6.opPattern","COPY",BODY,{"derivedFrom":makeQuery(id+"F1.opRevolve","SWEPT_BODY",BODY,{"disambiguationData":[OSD([sQuery(id+"F0.wireOp",EDGE,"E1")])]}),"instanceName":"1"}),"instanceName":"1"}),"instanceName":"1"}),"instanceName":"1"});
            var Q1357;
            Q1357=makeQuery(id+"F12.opPattern","COPY",BODY,{"derivedFrom":makeQuery(id+"F11.opPattern","COPY",BODY,{"derivedFrom":makeQuery(id+"F10.opPattern","COPY",BODY,{"derivedFrom":makeQuery(id+"F6.opPattern","COPY",BODY,{"derivedFrom":makeQuery(id+"F2.opPattern","COPY",BODY,{"derivedFrom":makeQuery(id+"F1.opRevolve","SWEPT_BODY",BODY,{"disambiguationData":[OSD([sQuery(id+"F0.wireOp",EDGE,"E1")])]}),"instanceName":"1"}),"instanceName":"1"}),"instanceName":"1"}),"instanceName":"1"}),"instanceName":"1"});
            var Q1358;
            Q1358=makeQuery(id+"F12.opPattern","COPY",BODY,{"derivedFrom":makeQuery(id+"F11.opPattern","COPY",BODY,{"derivedFrom":makeQuery(id+"F10.opPattern","COPY",BODY,{"derivedFrom":makeQuery(id+"F6.opPattern","COPY",BODY,{"derivedFrom":makeQuery(id+"F3.opPattern","COPY",BODY,{"derivedFrom":makeQuery(id+"F2.opPattern","COPY",BODY,{"derivedFrom":makeQuery(id+"F1.opRevolve","SWEPT_BODY",BODY,{"disambiguationData":[OSD([sQuery(id+"F0.wireOp",EDGE,"E1")])]}),"instanceName":"1"}),"instanceName":"1"}),"instanceName":"1"}),"instanceName":"1"}),"instanceName":"1"}),"instanceName":"1"});
            var Q1359;
            Q1359=makeQuery(id+"F12.opPattern","COPY",BODY,{"derivedFrom":makeQuery(id+"F11.opPattern","COPY",BODY,{"derivedFrom":makeQuery(id+"F10.opPattern","COPY",BODY,{"derivedFrom":makeQuery(id+"F6.opPattern","COPY",BODY,{"derivedFrom":makeQuery(id+"F4.opPattern","COPY",BODY,{"derivedFrom":makeQuery(id+"F1.opRevolve","SWEPT_BODY",BODY,{"disambiguationData":[OSD([sQuery(id+"F0.wireOp",EDGE,"E1")])]}),"instanceName":"1"}),"instanceName":"1"}),"instanceName":"1"}),"instanceName":"1"}),"instanceName":"1"});
            var Q1360;
            Q1360=makeQuery(id+"F12.opPattern","COPY",BODY,{"derivedFrom":makeQuery(id+"F11.opPattern","COPY",BODY,{"derivedFrom":makeQuery(id+"F10.opPattern","COPY",BODY,{"derivedFrom":makeQuery(id+"F6.opPattern","COPY",BODY,{"derivedFrom":makeQuery(id+"F4.opPattern","COPY",BODY,{"derivedFrom":makeQuery(id+"F2.opPattern","COPY",BODY,{"derivedFrom":makeQuery(id+"F1.opRevolve","SWEPT_BODY",BODY,{"disambiguationData":[OSD([sQuery(id+"F0.wireOp",EDGE,"E1")])]}),"instanceName":"1"}),"instanceName":"1"}),"instanceName":"1"}),"instanceName":"1"}),"instanceName":"1"}),"instanceName":"1"});
            var Q1361;
            Q1361=makeQuery(id+"F12.opPattern","COPY",BODY,{"derivedFrom":makeQuery(id+"F11.opPattern","COPY",BODY,{"derivedFrom":makeQuery(id+"F10.opPattern","COPY",BODY,{"derivedFrom":makeQuery(id+"F6.opPattern","COPY",BODY,{"derivedFrom":makeQuery(id+"F4.opPattern","COPY",BODY,{"derivedFrom":makeQuery(id+"F3.opPattern","COPY",BODY,{"derivedFrom":makeQuery(id+"F2.opPattern","COPY",BODY,{"derivedFrom":makeQuery(id+"F1.opRevolve","SWEPT_BODY",BODY,{"disambiguationData":[OSD([sQuery(id+"F0.wireOp",EDGE,"E1")])]}),"instanceName":"1"}),"instanceName":"1"}),"instanceName":"1"}),"instanceName":"1"}),"instanceName":"1"}),"instanceName":"1"}),"instanceName":"1"});
            var Q1362;
            Q1362=makeQuery(id+"F12.opPattern","COPY",BODY,{"derivedFrom":makeQuery(id+"F11.opPattern","COPY",BODY,{"derivedFrom":makeQuery(id+"F10.opPattern","COPY",BODY,{"derivedFrom":makeQuery(id+"F6.opPattern","COPY",BODY,{"derivedFrom":makeQuery(id+"F5.opPattern","COPY",BODY,{"derivedFrom":makeQuery(id+"F1.opRevolve","SWEPT_BODY",BODY,{"disambiguationData":[OSD([sQuery(id+"F0.wireOp",EDGE,"E1")])]}),"instanceName":"1"}),"instanceName":"1"}),"instanceName":"1"}),"instanceName":"1"}),"instanceName":"1"});
            var Q1363;
            Q1363=makeQuery(id+"F12.opPattern","COPY",BODY,{"derivedFrom":makeQuery(id+"F11.opPattern","COPY",BODY,{"derivedFrom":makeQuery(id+"F10.opPattern","COPY",BODY,{"derivedFrom":makeQuery(id+"F6.opPattern","COPY",BODY,{"derivedFrom":makeQuery(id+"F5.opPattern","COPY",BODY,{"derivedFrom":makeQuery(id+"F2.opPattern","COPY",BODY,{"derivedFrom":makeQuery(id+"F1.opRevolve","SWEPT_BODY",BODY,{"disambiguationData":[OSD([sQuery(id+"F0.wireOp",EDGE,"E1")])]}),"instanceName":"1"}),"instanceName":"1"}),"instanceName":"1"}),"instanceName":"1"}),"instanceName":"1"}),"instanceName":"1"});
            var Q1364;
            Q1364=makeQuery(id+"F12.opPattern","COPY",BODY,{"derivedFrom":makeQuery(id+"F11.opPattern","COPY",BODY,{"derivedFrom":makeQuery(id+"F10.opPattern","COPY",BODY,{"derivedFrom":makeQuery(id+"F6.opPattern","COPY",BODY,{"derivedFrom":makeQuery(id+"F5.opPattern","COPY",BODY,{"derivedFrom":makeQuery(id+"F3.opPattern","COPY",BODY,{"derivedFrom":makeQuery(id+"F2.opPattern","COPY",BODY,{"derivedFrom":makeQuery(id+"F1.opRevolve","SWEPT_BODY",BODY,{"disambiguationData":[OSD([sQuery(id+"F0.wireOp",EDGE,"E1")])]}),"instanceName":"1"}),"instanceName":"1"}),"instanceName":"1"}),"instanceName":"1"}),"instanceName":"1"}),"instanceName":"1"}),"instanceName":"1"});
            var Q1365;
            Q1365=makeQuery(id+"F12.opPattern","COPY",BODY,{"derivedFrom":makeQuery(id+"F11.opPattern","COPY",BODY,{"derivedFrom":makeQuery(id+"F10.opPattern","COPY",BODY,{"derivedFrom":makeQuery(id+"F6.opPattern","COPY",BODY,{"derivedFrom":makeQuery(id+"F5.opPattern","COPY",BODY,{"derivedFrom":makeQuery(id+"F4.opPattern","COPY",BODY,{"derivedFrom":makeQuery(id+"F1.opRevolve","SWEPT_BODY",BODY,{"disambiguationData":[OSD([sQuery(id+"F0.wireOp",EDGE,"E1")])]}),"instanceName":"1"}),"instanceName":"1"}),"instanceName":"1"}),"instanceName":"1"}),"instanceName":"1"}),"instanceName":"1"});
            var Q1366;
            Q1366=makeQuery(id+"F12.opPattern","COPY",BODY,{"derivedFrom":makeQuery(id+"F11.opPattern","COPY",BODY,{"derivedFrom":makeQuery(id+"F10.opPattern","COPY",BODY,{"derivedFrom":makeQuery(id+"F6.opPattern","COPY",BODY,{"derivedFrom":makeQuery(id+"F5.opPattern","COPY",BODY,{"derivedFrom":makeQuery(id+"F4.opPattern","COPY",BODY,{"derivedFrom":makeQuery(id+"F2.opPattern","COPY",BODY,{"derivedFrom":makeQuery(id+"F1.opRevolve","SWEPT_BODY",BODY,{"disambiguationData":[OSD([sQuery(id+"F0.wireOp",EDGE,"E1")])]}),"instanceName":"1"}),"instanceName":"1"}),"instanceName":"1"}),"instanceName":"1"}),"instanceName":"1"}),"instanceName":"1"}),"instanceName":"1"});
            var Q1367;
            Q1367=makeQuery(id+"F12.opPattern","COPY",BODY,{"derivedFrom":makeQuery(id+"F11.opPattern","COPY",BODY,{"derivedFrom":makeQuery(id+"F10.opPattern","COPY",BODY,{"derivedFrom":makeQuery(id+"F6.opPattern","COPY",BODY,{"derivedFrom":makeQuery(id+"F5.opPattern","COPY",BODY,{"derivedFrom":makeQuery(id+"F4.opPattern","COPY",BODY,{"derivedFrom":makeQuery(id+"F3.opPattern","COPY",BODY,{"derivedFrom":makeQuery(id+"F2.opPattern","COPY",BODY,{"derivedFrom":makeQuery(id+"F1.opRevolve","SWEPT_BODY",BODY,{"disambiguationData":[OSD([sQuery(id+"F0.wireOp",EDGE,"E1")])]}),"instanceName":"1"}),"instanceName":"1"}),"instanceName":"1"}),"instanceName":"1"}),"instanceName":"1"}),"instanceName":"1"}),"instanceName":"1"}),"instanceName":"1"});
            var Q1368;
            Q1368=makeQuery(id+"F12.opPattern","COPY",BODY,{"derivedFrom":makeQuery(id+"F11.opPattern","COPY",BODY,{"derivedFrom":makeQuery(id+"F10.opPattern","COPY",BODY,{"derivedFrom":makeQuery(id+"F7.opPattern","COPY",BODY,{"derivedFrom":makeQuery(id+"F1.opRevolve","SWEPT_BODY",BODY,{"disambiguationData":[OSD([sQuery(id+"F0.wireOp",EDGE,"E1")])]}),"instanceName":"1"}),"instanceName":"1"}),"instanceName":"1"}),"instanceName":"1"});
            var Q1369;
            Q1369=makeQuery(id+"F12.opPattern","COPY",BODY,{"derivedFrom":makeQuery(id+"F11.opPattern","COPY",BODY,{"derivedFrom":makeQuery(id+"F10.opPattern","COPY",BODY,{"derivedFrom":makeQuery(id+"F7.opPattern","COPY",BODY,{"derivedFrom":makeQuery(id+"F2.opPattern","COPY",BODY,{"derivedFrom":makeQuery(id+"F1.opRevolve","SWEPT_BODY",BODY,{"disambiguationData":[OSD([sQuery(id+"F0.wireOp",EDGE,"E1")])]}),"instanceName":"1"}),"instanceName":"1"}),"instanceName":"1"}),"instanceName":"1"}),"instanceName":"1"});
            var Q1370;
            Q1370=makeQuery(id+"F12.opPattern","COPY",BODY,{"derivedFrom":makeQuery(id+"F11.opPattern","COPY",BODY,{"derivedFrom":makeQuery(id+"F10.opPattern","COPY",BODY,{"derivedFrom":makeQuery(id+"F7.opPattern","COPY",BODY,{"derivedFrom":makeQuery(id+"F3.opPattern","COPY",BODY,{"derivedFrom":makeQuery(id+"F2.opPattern","COPY",BODY,{"derivedFrom":makeQuery(id+"F1.opRevolve","SWEPT_BODY",BODY,{"disambiguationData":[OSD([sQuery(id+"F0.wireOp",EDGE,"E1")])]}),"instanceName":"1"}),"instanceName":"1"}),"instanceName":"1"}),"instanceName":"1"}),"instanceName":"1"}),"instanceName":"1"});
            var Q1371;
            Q1371=makeQuery(id+"F12.opPattern","COPY",BODY,{"derivedFrom":makeQuery(id+"F11.opPattern","COPY",BODY,{"derivedFrom":makeQuery(id+"F10.opPattern","COPY",BODY,{"derivedFrom":makeQuery(id+"F7.opPattern","COPY",BODY,{"derivedFrom":makeQuery(id+"F4.opPattern","COPY",BODY,{"derivedFrom":makeQuery(id+"F1.opRevolve","SWEPT_BODY",BODY,{"disambiguationData":[OSD([sQuery(id+"F0.wireOp",EDGE,"E1")])]}),"instanceName":"1"}),"instanceName":"1"}),"instanceName":"1"}),"instanceName":"1"}),"instanceName":"1"});
            var Q1372;
            Q1372=makeQuery(id+"F12.opPattern","COPY",BODY,{"derivedFrom":makeQuery(id+"F11.opPattern","COPY",BODY,{"derivedFrom":makeQuery(id+"F10.opPattern","COPY",BODY,{"derivedFrom":makeQuery(id+"F7.opPattern","COPY",BODY,{"derivedFrom":makeQuery(id+"F4.opPattern","COPY",BODY,{"derivedFrom":makeQuery(id+"F2.opPattern","COPY",BODY,{"derivedFrom":makeQuery(id+"F1.opRevolve","SWEPT_BODY",BODY,{"disambiguationData":[OSD([sQuery(id+"F0.wireOp",EDGE,"E1")])]}),"instanceName":"1"}),"instanceName":"1"}),"instanceName":"1"}),"instanceName":"1"}),"instanceName":"1"}),"instanceName":"1"});
            var Q1373;
            Q1373=makeQuery(id+"F12.opPattern","COPY",BODY,{"derivedFrom":makeQuery(id+"F11.opPattern","COPY",BODY,{"derivedFrom":makeQuery(id+"F10.opPattern","COPY",BODY,{"derivedFrom":makeQuery(id+"F7.opPattern","COPY",BODY,{"derivedFrom":makeQuery(id+"F4.opPattern","COPY",BODY,{"derivedFrom":makeQuery(id+"F3.opPattern","COPY",BODY,{"derivedFrom":makeQuery(id+"F2.opPattern","COPY",BODY,{"derivedFrom":makeQuery(id+"F1.opRevolve","SWEPT_BODY",BODY,{"disambiguationData":[OSD([sQuery(id+"F0.wireOp",EDGE,"E1")])]}),"instanceName":"1"}),"instanceName":"1"}),"instanceName":"1"}),"instanceName":"1"}),"instanceName":"1"}),"instanceName":"1"}),"instanceName":"1"});
            var Q1374;
            Q1374=makeQuery(id+"F12.opPattern","COPY",BODY,{"derivedFrom":makeQuery(id+"F11.opPattern","COPY",BODY,{"derivedFrom":makeQuery(id+"F10.opPattern","COPY",BODY,{"derivedFrom":makeQuery(id+"F7.opPattern","COPY",BODY,{"derivedFrom":makeQuery(id+"F5.opPattern","COPY",BODY,{"derivedFrom":makeQuery(id+"F1.opRevolve","SWEPT_BODY",BODY,{"disambiguationData":[OSD([sQuery(id+"F0.wireOp",EDGE,"E1")])]}),"instanceName":"1"}),"instanceName":"1"}),"instanceName":"1"}),"instanceName":"1"}),"instanceName":"1"});
            var Q1375;
            Q1375=makeQuery(id+"F12.opPattern","COPY",BODY,{"derivedFrom":makeQuery(id+"F11.opPattern","COPY",BODY,{"derivedFrom":makeQuery(id+"F10.opPattern","COPY",BODY,{"derivedFrom":makeQuery(id+"F7.opPattern","COPY",BODY,{"derivedFrom":makeQuery(id+"F5.opPattern","COPY",BODY,{"derivedFrom":makeQuery(id+"F2.opPattern","COPY",BODY,{"derivedFrom":makeQuery(id+"F1.opRevolve","SWEPT_BODY",BODY,{"disambiguationData":[OSD([sQuery(id+"F0.wireOp",EDGE,"E1")])]}),"instanceName":"1"}),"instanceName":"1"}),"instanceName":"1"}),"instanceName":"1"}),"instanceName":"1"}),"instanceName":"1"});
            var Q1376;
            Q1376=makeQuery(id+"F12.opPattern","COPY",BODY,{"derivedFrom":makeQuery(id+"F11.opPattern","COPY",BODY,{"derivedFrom":makeQuery(id+"F10.opPattern","COPY",BODY,{"derivedFrom":makeQuery(id+"F7.opPattern","COPY",BODY,{"derivedFrom":makeQuery(id+"F5.opPattern","COPY",BODY,{"derivedFrom":makeQuery(id+"F3.opPattern","COPY",BODY,{"derivedFrom":makeQuery(id+"F2.opPattern","COPY",BODY,{"derivedFrom":makeQuery(id+"F1.opRevolve","SWEPT_BODY",BODY,{"disambiguationData":[OSD([sQuery(id+"F0.wireOp",EDGE,"E1")])]}),"instanceName":"1"}),"instanceName":"1"}),"instanceName":"1"}),"instanceName":"1"}),"instanceName":"1"}),"instanceName":"1"}),"instanceName":"1"});
            var Q1377;
            Q1377=makeQuery(id+"F12.opPattern","COPY",BODY,{"derivedFrom":makeQuery(id+"F11.opPattern","COPY",BODY,{"derivedFrom":makeQuery(id+"F10.opPattern","COPY",BODY,{"derivedFrom":makeQuery(id+"F7.opPattern","COPY",BODY,{"derivedFrom":makeQuery(id+"F5.opPattern","COPY",BODY,{"derivedFrom":makeQuery(id+"F4.opPattern","COPY",BODY,{"derivedFrom":makeQuery(id+"F1.opRevolve","SWEPT_BODY",BODY,{"disambiguationData":[OSD([sQuery(id+"F0.wireOp",EDGE,"E1")])]}),"instanceName":"1"}),"instanceName":"1"}),"instanceName":"1"}),"instanceName":"1"}),"instanceName":"1"}),"instanceName":"1"});
            var Q1378;
            Q1378=makeQuery(id+"F12.opPattern","COPY",BODY,{"derivedFrom":makeQuery(id+"F11.opPattern","COPY",BODY,{"derivedFrom":makeQuery(id+"F10.opPattern","COPY",BODY,{"derivedFrom":makeQuery(id+"F7.opPattern","COPY",BODY,{"derivedFrom":makeQuery(id+"F5.opPattern","COPY",BODY,{"derivedFrom":makeQuery(id+"F4.opPattern","COPY",BODY,{"derivedFrom":makeQuery(id+"F2.opPattern","COPY",BODY,{"derivedFrom":makeQuery(id+"F1.opRevolve","SWEPT_BODY",BODY,{"disambiguationData":[OSD([sQuery(id+"F0.wireOp",EDGE,"E1")])]}),"instanceName":"1"}),"instanceName":"1"}),"instanceName":"1"}),"instanceName":"1"}),"instanceName":"1"}),"instanceName":"1"}),"instanceName":"1"});
            var Q1379;
            Q1379=makeQuery(id+"F12.opPattern","COPY",BODY,{"derivedFrom":makeQuery(id+"F11.opPattern","COPY",BODY,{"derivedFrom":makeQuery(id+"F10.opPattern","COPY",BODY,{"derivedFrom":makeQuery(id+"F7.opPattern","COPY",BODY,{"derivedFrom":makeQuery(id+"F5.opPattern","COPY",BODY,{"derivedFrom":makeQuery(id+"F4.opPattern","COPY",BODY,{"derivedFrom":makeQuery(id+"F3.opPattern","COPY",BODY,{"derivedFrom":makeQuery(id+"F2.opPattern","COPY",BODY,{"derivedFrom":makeQuery(id+"F1.opRevolve","SWEPT_BODY",BODY,{"disambiguationData":[OSD([sQuery(id+"F0.wireOp",EDGE,"E1")])]}),"instanceName":"1"}),"instanceName":"1"}),"instanceName":"1"}),"instanceName":"1"}),"instanceName":"1"}),"instanceName":"1"}),"instanceName":"1"}),"instanceName":"1"});
            var Q1380;
            Q1380=makeQuery(id+"F12.opPattern","COPY",BODY,{"derivedFrom":makeQuery(id+"F11.opPattern","COPY",BODY,{"derivedFrom":makeQuery(id+"F10.opPattern","COPY",BODY,{"derivedFrom":makeQuery(id+"F7.opPattern","COPY",BODY,{"derivedFrom":makeQuery(id+"F6.opPattern","COPY",BODY,{"derivedFrom":makeQuery(id+"F1.opRevolve","SWEPT_BODY",BODY,{"disambiguationData":[OSD([sQuery(id+"F0.wireOp",EDGE,"E1")])]}),"instanceName":"1"}),"instanceName":"1"}),"instanceName":"1"}),"instanceName":"1"}),"instanceName":"1"});
            var Q1381;
            Q1381=makeQuery(id+"F12.opPattern","COPY",BODY,{"derivedFrom":makeQuery(id+"F11.opPattern","COPY",BODY,{"derivedFrom":makeQuery(id+"F10.opPattern","COPY",BODY,{"derivedFrom":makeQuery(id+"F7.opPattern","COPY",BODY,{"derivedFrom":makeQuery(id+"F6.opPattern","COPY",BODY,{"derivedFrom":makeQuery(id+"F2.opPattern","COPY",BODY,{"derivedFrom":makeQuery(id+"F1.opRevolve","SWEPT_BODY",BODY,{"disambiguationData":[OSD([sQuery(id+"F0.wireOp",EDGE,"E1")])]}),"instanceName":"1"}),"instanceName":"1"}),"instanceName":"1"}),"instanceName":"1"}),"instanceName":"1"}),"instanceName":"1"});
            var Q1382;
            Q1382=makeQuery(id+"F12.opPattern","COPY",BODY,{"derivedFrom":makeQuery(id+"F11.opPattern","COPY",BODY,{"derivedFrom":makeQuery(id+"F10.opPattern","COPY",BODY,{"derivedFrom":makeQuery(id+"F7.opPattern","COPY",BODY,{"derivedFrom":makeQuery(id+"F6.opPattern","COPY",BODY,{"derivedFrom":makeQuery(id+"F3.opPattern","COPY",BODY,{"derivedFrom":makeQuery(id+"F2.opPattern","COPY",BODY,{"derivedFrom":makeQuery(id+"F1.opRevolve","SWEPT_BODY",BODY,{"disambiguationData":[OSD([sQuery(id+"F0.wireOp",EDGE,"E1")])]}),"instanceName":"1"}),"instanceName":"1"}),"instanceName":"1"}),"instanceName":"1"}),"instanceName":"1"}),"instanceName":"1"}),"instanceName":"1"});
            var Q1383;
            Q1383=makeQuery(id+"F12.opPattern","COPY",BODY,{"derivedFrom":makeQuery(id+"F11.opPattern","COPY",BODY,{"derivedFrom":makeQuery(id+"F10.opPattern","COPY",BODY,{"derivedFrom":makeQuery(id+"F7.opPattern","COPY",BODY,{"derivedFrom":makeQuery(id+"F6.opPattern","COPY",BODY,{"derivedFrom":makeQuery(id+"F4.opPattern","COPY",BODY,{"derivedFrom":makeQuery(id+"F1.opRevolve","SWEPT_BODY",BODY,{"disambiguationData":[OSD([sQuery(id+"F0.wireOp",EDGE,"E1")])]}),"instanceName":"1"}),"instanceName":"1"}),"instanceName":"1"}),"instanceName":"1"}),"instanceName":"1"}),"instanceName":"1"});
            var Q1384;
            Q1384=makeQuery(id+"F12.opPattern","COPY",BODY,{"derivedFrom":makeQuery(id+"F11.opPattern","COPY",BODY,{"derivedFrom":makeQuery(id+"F10.opPattern","COPY",BODY,{"derivedFrom":makeQuery(id+"F7.opPattern","COPY",BODY,{"derivedFrom":makeQuery(id+"F6.opPattern","COPY",BODY,{"derivedFrom":makeQuery(id+"F4.opPattern","COPY",BODY,{"derivedFrom":makeQuery(id+"F2.opPattern","COPY",BODY,{"derivedFrom":makeQuery(id+"F1.opRevolve","SWEPT_BODY",BODY,{"disambiguationData":[OSD([sQuery(id+"F0.wireOp",EDGE,"E1")])]}),"instanceName":"1"}),"instanceName":"1"}),"instanceName":"1"}),"instanceName":"1"}),"instanceName":"1"}),"instanceName":"1"}),"instanceName":"1"});
            var Q1385;
            Q1385=makeQuery(id+"F12.opPattern","COPY",BODY,{"derivedFrom":makeQuery(id+"F11.opPattern","COPY",BODY,{"derivedFrom":makeQuery(id+"F10.opPattern","COPY",BODY,{"derivedFrom":makeQuery(id+"F7.opPattern","COPY",BODY,{"derivedFrom":makeQuery(id+"F6.opPattern","COPY",BODY,{"derivedFrom":makeQuery(id+"F4.opPattern","COPY",BODY,{"derivedFrom":makeQuery(id+"F3.opPattern","COPY",BODY,{"derivedFrom":makeQuery(id+"F2.opPattern","COPY",BODY,{"derivedFrom":makeQuery(id+"F1.opRevolve","SWEPT_BODY",BODY,{"disambiguationData":[OSD([sQuery(id+"F0.wireOp",EDGE,"E1")])]}),"instanceName":"1"}),"instanceName":"1"}),"instanceName":"1"}),"instanceName":"1"}),"instanceName":"1"}),"instanceName":"1"}),"instanceName":"1"}),"instanceName":"1"});
            var Q1386;
            Q1386=makeQuery(id+"F12.opPattern","COPY",BODY,{"derivedFrom":makeQuery(id+"F11.opPattern","COPY",BODY,{"derivedFrom":makeQuery(id+"F10.opPattern","COPY",BODY,{"derivedFrom":makeQuery(id+"F7.opPattern","COPY",BODY,{"derivedFrom":makeQuery(id+"F6.opPattern","COPY",BODY,{"derivedFrom":makeQuery(id+"F5.opPattern","COPY",BODY,{"derivedFrom":makeQuery(id+"F1.opRevolve","SWEPT_BODY",BODY,{"disambiguationData":[OSD([sQuery(id+"F0.wireOp",EDGE,"E1")])]}),"instanceName":"1"}),"instanceName":"1"}),"instanceName":"1"}),"instanceName":"1"}),"instanceName":"1"}),"instanceName":"1"});
            var Q1387;
            Q1387=makeQuery(id+"F12.opPattern","COPY",BODY,{"derivedFrom":makeQuery(id+"F11.opPattern","COPY",BODY,{"derivedFrom":makeQuery(id+"F10.opPattern","COPY",BODY,{"derivedFrom":makeQuery(id+"F7.opPattern","COPY",BODY,{"derivedFrom":makeQuery(id+"F6.opPattern","COPY",BODY,{"derivedFrom":makeQuery(id+"F5.opPattern","COPY",BODY,{"derivedFrom":makeQuery(id+"F2.opPattern","COPY",BODY,{"derivedFrom":makeQuery(id+"F1.opRevolve","SWEPT_BODY",BODY,{"disambiguationData":[OSD([sQuery(id+"F0.wireOp",EDGE,"E1")])]}),"instanceName":"1"}),"instanceName":"1"}),"instanceName":"1"}),"instanceName":"1"}),"instanceName":"1"}),"instanceName":"1"}),"instanceName":"1"});
            var Q1388;
            Q1388=makeQuery(id+"F12.opPattern","COPY",BODY,{"derivedFrom":makeQuery(id+"F11.opPattern","COPY",BODY,{"derivedFrom":makeQuery(id+"F10.opPattern","COPY",BODY,{"derivedFrom":makeQuery(id+"F7.opPattern","COPY",BODY,{"derivedFrom":makeQuery(id+"F6.opPattern","COPY",BODY,{"derivedFrom":makeQuery(id+"F5.opPattern","COPY",BODY,{"derivedFrom":makeQuery(id+"F3.opPattern","COPY",BODY,{"derivedFrom":makeQuery(id+"F2.opPattern","COPY",BODY,{"derivedFrom":makeQuery(id+"F1.opRevolve","SWEPT_BODY",BODY,{"disambiguationData":[OSD([sQuery(id+"F0.wireOp",EDGE,"E1")])]}),"instanceName":"1"}),"instanceName":"1"}),"instanceName":"1"}),"instanceName":"1"}),"instanceName":"1"}),"instanceName":"1"}),"instanceName":"1"}),"instanceName":"1"});
            var Q1389;
            Q1389=makeQuery(id+"F12.opPattern","COPY",BODY,{"derivedFrom":makeQuery(id+"F11.opPattern","COPY",BODY,{"derivedFrom":makeQuery(id+"F10.opPattern","COPY",BODY,{"derivedFrom":makeQuery(id+"F7.opPattern","COPY",BODY,{"derivedFrom":makeQuery(id+"F6.opPattern","COPY",BODY,{"derivedFrom":makeQuery(id+"F5.opPattern","COPY",BODY,{"derivedFrom":makeQuery(id+"F4.opPattern","COPY",BODY,{"derivedFrom":makeQuery(id+"F1.opRevolve","SWEPT_BODY",BODY,{"disambiguationData":[OSD([sQuery(id+"F0.wireOp",EDGE,"E1")])]}),"instanceName":"1"}),"instanceName":"1"}),"instanceName":"1"}),"instanceName":"1"}),"instanceName":"1"}),"instanceName":"1"}),"instanceName":"1"});
            var Q1390;
            Q1390=makeQuery(id+"F12.opPattern","COPY",BODY,{"derivedFrom":makeQuery(id+"F11.opPattern","COPY",BODY,{"derivedFrom":makeQuery(id+"F10.opPattern","COPY",BODY,{"derivedFrom":makeQuery(id+"F7.opPattern","COPY",BODY,{"derivedFrom":makeQuery(id+"F6.opPattern","COPY",BODY,{"derivedFrom":makeQuery(id+"F5.opPattern","COPY",BODY,{"derivedFrom":makeQuery(id+"F4.opPattern","COPY",BODY,{"derivedFrom":makeQuery(id+"F2.opPattern","COPY",BODY,{"derivedFrom":makeQuery(id+"F1.opRevolve","SWEPT_BODY",BODY,{"disambiguationData":[OSD([sQuery(id+"F0.wireOp",EDGE,"E1")])]}),"instanceName":"1"}),"instanceName":"1"}),"instanceName":"1"}),"instanceName":"1"}),"instanceName":"1"}),"instanceName":"1"}),"instanceName":"1"}),"instanceName":"1"});
            var Q1391;
            Q1391=makeQuery(id+"F12.opPattern","COPY",BODY,{"derivedFrom":makeQuery(id+"F11.opPattern","COPY",BODY,{"derivedFrom":makeQuery(id+"F10.opPattern","COPY",BODY,{"derivedFrom":makeQuery(id+"F7.opPattern","COPY",BODY,{"derivedFrom":makeQuery(id+"F6.opPattern","COPY",BODY,{"derivedFrom":makeQuery(id+"F5.opPattern","COPY",BODY,{"derivedFrom":makeQuery(id+"F4.opPattern","COPY",BODY,{"derivedFrom":makeQuery(id+"F3.opPattern","COPY",BODY,{"derivedFrom":makeQuery(id+"F2.opPattern","COPY",BODY,{"derivedFrom":makeQuery(id+"F1.opRevolve","SWEPT_BODY",BODY,{"disambiguationData":[OSD([sQuery(id+"F0.wireOp",EDGE,"E1")])]}),"instanceName":"1"}),"instanceName":"1"}),"instanceName":"1"}),"instanceName":"1"}),"instanceName":"1"}),"instanceName":"1"}),"instanceName":"1"}),"instanceName":"1"}),"instanceName":"1"});
            var Q1392;
            Q1392=makeQuery(id+"F12.opPattern","COPY",BODY,{"derivedFrom":makeQuery(id+"F11.opPattern","COPY",BODY,{"derivedFrom":makeQuery(id+"F10.opPattern","COPY",BODY,{"derivedFrom":makeQuery(id+"F8.opPattern","COPY",BODY,{"derivedFrom":makeQuery(id+"F1.opRevolve","SWEPT_BODY",BODY,{"disambiguationData":[OSD([sQuery(id+"F0.wireOp",EDGE,"E1")])]}),"instanceName":"1"}),"instanceName":"1"}),"instanceName":"1"}),"instanceName":"1"});
            var Q1393;
            Q1393=makeQuery(id+"F12.opPattern","COPY",BODY,{"derivedFrom":makeQuery(id+"F11.opPattern","COPY",BODY,{"derivedFrom":makeQuery(id+"F10.opPattern","COPY",BODY,{"derivedFrom":makeQuery(id+"F8.opPattern","COPY",BODY,{"derivedFrom":makeQuery(id+"F2.opPattern","COPY",BODY,{"derivedFrom":makeQuery(id+"F1.opRevolve","SWEPT_BODY",BODY,{"disambiguationData":[OSD([sQuery(id+"F0.wireOp",EDGE,"E1")])]}),"instanceName":"1"}),"instanceName":"1"}),"instanceName":"1"}),"instanceName":"1"}),"instanceName":"1"});
            var Q1394;
            Q1394=makeQuery(id+"F12.opPattern","COPY",BODY,{"derivedFrom":makeQuery(id+"F11.opPattern","COPY",BODY,{"derivedFrom":makeQuery(id+"F10.opPattern","COPY",BODY,{"derivedFrom":makeQuery(id+"F8.opPattern","COPY",BODY,{"derivedFrom":makeQuery(id+"F3.opPattern","COPY",BODY,{"derivedFrom":makeQuery(id+"F2.opPattern","COPY",BODY,{"derivedFrom":makeQuery(id+"F1.opRevolve","SWEPT_BODY",BODY,{"disambiguationData":[OSD([sQuery(id+"F0.wireOp",EDGE,"E1")])]}),"instanceName":"1"}),"instanceName":"1"}),"instanceName":"1"}),"instanceName":"1"}),"instanceName":"1"}),"instanceName":"1"});
            var Q1395;
            Q1395=makeQuery(id+"F12.opPattern","COPY",BODY,{"derivedFrom":makeQuery(id+"F11.opPattern","COPY",BODY,{"derivedFrom":makeQuery(id+"F10.opPattern","COPY",BODY,{"derivedFrom":makeQuery(id+"F8.opPattern","COPY",BODY,{"derivedFrom":makeQuery(id+"F4.opPattern","COPY",BODY,{"derivedFrom":makeQuery(id+"F1.opRevolve","SWEPT_BODY",BODY,{"disambiguationData":[OSD([sQuery(id+"F0.wireOp",EDGE,"E1")])]}),"instanceName":"1"}),"instanceName":"1"}),"instanceName":"1"}),"instanceName":"1"}),"instanceName":"1"});
            var Q1396;
            Q1396=makeQuery(id+"F12.opPattern","COPY",BODY,{"derivedFrom":makeQuery(id+"F11.opPattern","COPY",BODY,{"derivedFrom":makeQuery(id+"F10.opPattern","COPY",BODY,{"derivedFrom":makeQuery(id+"F8.opPattern","COPY",BODY,{"derivedFrom":makeQuery(id+"F4.opPattern","COPY",BODY,{"derivedFrom":makeQuery(id+"F2.opPattern","COPY",BODY,{"derivedFrom":makeQuery(id+"F1.opRevolve","SWEPT_BODY",BODY,{"disambiguationData":[OSD([sQuery(id+"F0.wireOp",EDGE,"E1")])]}),"instanceName":"1"}),"instanceName":"1"}),"instanceName":"1"}),"instanceName":"1"}),"instanceName":"1"}),"instanceName":"1"});
            var Q1397;
            Q1397=makeQuery(id+"F12.opPattern","COPY",BODY,{"derivedFrom":makeQuery(id+"F11.opPattern","COPY",BODY,{"derivedFrom":makeQuery(id+"F10.opPattern","COPY",BODY,{"derivedFrom":makeQuery(id+"F8.opPattern","COPY",BODY,{"derivedFrom":makeQuery(id+"F4.opPattern","COPY",BODY,{"derivedFrom":makeQuery(id+"F3.opPattern","COPY",BODY,{"derivedFrom":makeQuery(id+"F2.opPattern","COPY",BODY,{"derivedFrom":makeQuery(id+"F1.opRevolve","SWEPT_BODY",BODY,{"disambiguationData":[OSD([sQuery(id+"F0.wireOp",EDGE,"E1")])]}),"instanceName":"1"}),"instanceName":"1"}),"instanceName":"1"}),"instanceName":"1"}),"instanceName":"1"}),"instanceName":"1"}),"instanceName":"1"});
            var Q1398;
            Q1398=makeQuery(id+"F12.opPattern","COPY",BODY,{"derivedFrom":makeQuery(id+"F11.opPattern","COPY",BODY,{"derivedFrom":makeQuery(id+"F10.opPattern","COPY",BODY,{"derivedFrom":makeQuery(id+"F8.opPattern","COPY",BODY,{"derivedFrom":makeQuery(id+"F5.opPattern","COPY",BODY,{"derivedFrom":makeQuery(id+"F1.opRevolve","SWEPT_BODY",BODY,{"disambiguationData":[OSD([sQuery(id+"F0.wireOp",EDGE,"E1")])]}),"instanceName":"1"}),"instanceName":"1"}),"instanceName":"1"}),"instanceName":"1"}),"instanceName":"1"});
            var Q1399;
            Q1399=makeQuery(id+"F12.opPattern","COPY",BODY,{"derivedFrom":makeQuery(id+"F11.opPattern","COPY",BODY,{"derivedFrom":makeQuery(id+"F10.opPattern","COPY",BODY,{"derivedFrom":makeQuery(id+"F8.opPattern","COPY",BODY,{"derivedFrom":makeQuery(id+"F5.opPattern","COPY",BODY,{"derivedFrom":makeQuery(id+"F2.opPattern","COPY",BODY,{"derivedFrom":makeQuery(id+"F1.opRevolve","SWEPT_BODY",BODY,{"disambiguationData":[OSD([sQuery(id+"F0.wireOp",EDGE,"E1")])]}),"instanceName":"1"}),"instanceName":"1"}),"instanceName":"1"}),"instanceName":"1"}),"instanceName":"1"}),"instanceName":"1"});
            var Q1400;
            Q1400=makeQuery(id+"F12.opPattern","COPY",BODY,{"derivedFrom":makeQuery(id+"F11.opPattern","COPY",BODY,{"derivedFrom":makeQuery(id+"F10.opPattern","COPY",BODY,{"derivedFrom":makeQuery(id+"F8.opPattern","COPY",BODY,{"derivedFrom":makeQuery(id+"F5.opPattern","COPY",BODY,{"derivedFrom":makeQuery(id+"F3.opPattern","COPY",BODY,{"derivedFrom":makeQuery(id+"F2.opPattern","COPY",BODY,{"derivedFrom":makeQuery(id+"F1.opRevolve","SWEPT_BODY",BODY,{"disambiguationData":[OSD([sQuery(id+"F0.wireOp",EDGE,"E1")])]}),"instanceName":"1"}),"instanceName":"1"}),"instanceName":"1"}),"instanceName":"1"}),"instanceName":"1"}),"instanceName":"1"}),"instanceName":"1"});
            var Q1401;
            Q1401=makeQuery(id+"F12.opPattern","COPY",BODY,{"derivedFrom":makeQuery(id+"F11.opPattern","COPY",BODY,{"derivedFrom":makeQuery(id+"F10.opPattern","COPY",BODY,{"derivedFrom":makeQuery(id+"F8.opPattern","COPY",BODY,{"derivedFrom":makeQuery(id+"F5.opPattern","COPY",BODY,{"derivedFrom":makeQuery(id+"F4.opPattern","COPY",BODY,{"derivedFrom":makeQuery(id+"F1.opRevolve","SWEPT_BODY",BODY,{"disambiguationData":[OSD([sQuery(id+"F0.wireOp",EDGE,"E1")])]}),"instanceName":"1"}),"instanceName":"1"}),"instanceName":"1"}),"instanceName":"1"}),"instanceName":"1"}),"instanceName":"1"});
            var Q1402;
            Q1402=makeQuery(id+"F12.opPattern","COPY",BODY,{"derivedFrom":makeQuery(id+"F11.opPattern","COPY",BODY,{"derivedFrom":makeQuery(id+"F10.opPattern","COPY",BODY,{"derivedFrom":makeQuery(id+"F8.opPattern","COPY",BODY,{"derivedFrom":makeQuery(id+"F5.opPattern","COPY",BODY,{"derivedFrom":makeQuery(id+"F4.opPattern","COPY",BODY,{"derivedFrom":makeQuery(id+"F2.opPattern","COPY",BODY,{"derivedFrom":makeQuery(id+"F1.opRevolve","SWEPT_BODY",BODY,{"disambiguationData":[OSD([sQuery(id+"F0.wireOp",EDGE,"E1")])]}),"instanceName":"1"}),"instanceName":"1"}),"instanceName":"1"}),"instanceName":"1"}),"instanceName":"1"}),"instanceName":"1"}),"instanceName":"1"});
            var Q1403;
            Q1403=makeQuery(id+"F12.opPattern","COPY",BODY,{"derivedFrom":makeQuery(id+"F11.opPattern","COPY",BODY,{"derivedFrom":makeQuery(id+"F10.opPattern","COPY",BODY,{"derivedFrom":makeQuery(id+"F8.opPattern","COPY",BODY,{"derivedFrom":makeQuery(id+"F5.opPattern","COPY",BODY,{"derivedFrom":makeQuery(id+"F4.opPattern","COPY",BODY,{"derivedFrom":makeQuery(id+"F3.opPattern","COPY",BODY,{"derivedFrom":makeQuery(id+"F2.opPattern","COPY",BODY,{"derivedFrom":makeQuery(id+"F1.opRevolve","SWEPT_BODY",BODY,{"disambiguationData":[OSD([sQuery(id+"F0.wireOp",EDGE,"E1")])]}),"instanceName":"1"}),"instanceName":"1"}),"instanceName":"1"}),"instanceName":"1"}),"instanceName":"1"}),"instanceName":"1"}),"instanceName":"1"}),"instanceName":"1"});
            var Q1404;
            Q1404=makeQuery(id+"F12.opPattern","COPY",BODY,{"derivedFrom":makeQuery(id+"F11.opPattern","COPY",BODY,{"derivedFrom":makeQuery(id+"F10.opPattern","COPY",BODY,{"derivedFrom":makeQuery(id+"F8.opPattern","COPY",BODY,{"derivedFrom":makeQuery(id+"F6.opPattern","COPY",BODY,{"derivedFrom":makeQuery(id+"F1.opRevolve","SWEPT_BODY",BODY,{"disambiguationData":[OSD([sQuery(id+"F0.wireOp",EDGE,"E1")])]}),"instanceName":"1"}),"instanceName":"1"}),"instanceName":"1"}),"instanceName":"1"}),"instanceName":"1"});
            var Q1405;
            Q1405=makeQuery(id+"F12.opPattern","COPY",BODY,{"derivedFrom":makeQuery(id+"F11.opPattern","COPY",BODY,{"derivedFrom":makeQuery(id+"F10.opPattern","COPY",BODY,{"derivedFrom":makeQuery(id+"F8.opPattern","COPY",BODY,{"derivedFrom":makeQuery(id+"F6.opPattern","COPY",BODY,{"derivedFrom":makeQuery(id+"F2.opPattern","COPY",BODY,{"derivedFrom":makeQuery(id+"F1.opRevolve","SWEPT_BODY",BODY,{"disambiguationData":[OSD([sQuery(id+"F0.wireOp",EDGE,"E1")])]}),"instanceName":"1"}),"instanceName":"1"}),"instanceName":"1"}),"instanceName":"1"}),"instanceName":"1"}),"instanceName":"1"});
            var Q1406;
            Q1406=makeQuery(id+"F12.opPattern","COPY",BODY,{"derivedFrom":makeQuery(id+"F11.opPattern","COPY",BODY,{"derivedFrom":makeQuery(id+"F10.opPattern","COPY",BODY,{"derivedFrom":makeQuery(id+"F8.opPattern","COPY",BODY,{"derivedFrom":makeQuery(id+"F6.opPattern","COPY",BODY,{"derivedFrom":makeQuery(id+"F3.opPattern","COPY",BODY,{"derivedFrom":makeQuery(id+"F2.opPattern","COPY",BODY,{"derivedFrom":makeQuery(id+"F1.opRevolve","SWEPT_BODY",BODY,{"disambiguationData":[OSD([sQuery(id+"F0.wireOp",EDGE,"E1")])]}),"instanceName":"1"}),"instanceName":"1"}),"instanceName":"1"}),"instanceName":"1"}),"instanceName":"1"}),"instanceName":"1"}),"instanceName":"1"});
            var Q1407;
            Q1407=makeQuery(id+"F12.opPattern","COPY",BODY,{"derivedFrom":makeQuery(id+"F11.opPattern","COPY",BODY,{"derivedFrom":makeQuery(id+"F10.opPattern","COPY",BODY,{"derivedFrom":makeQuery(id+"F8.opPattern","COPY",BODY,{"derivedFrom":makeQuery(id+"F6.opPattern","COPY",BODY,{"derivedFrom":makeQuery(id+"F4.opPattern","COPY",BODY,{"derivedFrom":makeQuery(id+"F1.opRevolve","SWEPT_BODY",BODY,{"disambiguationData":[OSD([sQuery(id+"F0.wireOp",EDGE,"E1")])]}),"instanceName":"1"}),"instanceName":"1"}),"instanceName":"1"}),"instanceName":"1"}),"instanceName":"1"}),"instanceName":"1"});
            var Q1408;
            Q1408=makeQuery(id+"F12.opPattern","COPY",BODY,{"derivedFrom":makeQuery(id+"F11.opPattern","COPY",BODY,{"derivedFrom":makeQuery(id+"F10.opPattern","COPY",BODY,{"derivedFrom":makeQuery(id+"F8.opPattern","COPY",BODY,{"derivedFrom":makeQuery(id+"F6.opPattern","COPY",BODY,{"derivedFrom":makeQuery(id+"F4.opPattern","COPY",BODY,{"derivedFrom":makeQuery(id+"F2.opPattern","COPY",BODY,{"derivedFrom":makeQuery(id+"F1.opRevolve","SWEPT_BODY",BODY,{"disambiguationData":[OSD([sQuery(id+"F0.wireOp",EDGE,"E1")])]}),"instanceName":"1"}),"instanceName":"1"}),"instanceName":"1"}),"instanceName":"1"}),"instanceName":"1"}),"instanceName":"1"}),"instanceName":"1"});
            var Q1409;
            Q1409=makeQuery(id+"F12.opPattern","COPY",BODY,{"derivedFrom":makeQuery(id+"F11.opPattern","COPY",BODY,{"derivedFrom":makeQuery(id+"F10.opPattern","COPY",BODY,{"derivedFrom":makeQuery(id+"F8.opPattern","COPY",BODY,{"derivedFrom":makeQuery(id+"F6.opPattern","COPY",BODY,{"derivedFrom":makeQuery(id+"F4.opPattern","COPY",BODY,{"derivedFrom":makeQuery(id+"F3.opPattern","COPY",BODY,{"derivedFrom":makeQuery(id+"F2.opPattern","COPY",BODY,{"derivedFrom":makeQuery(id+"F1.opRevolve","SWEPT_BODY",BODY,{"disambiguationData":[OSD([sQuery(id+"F0.wireOp",EDGE,"E1")])]}),"instanceName":"1"}),"instanceName":"1"}),"instanceName":"1"}),"instanceName":"1"}),"instanceName":"1"}),"instanceName":"1"}),"instanceName":"1"}),"instanceName":"1"});
            var Q1410;
            Q1410=makeQuery(id+"F12.opPattern","COPY",BODY,{"derivedFrom":makeQuery(id+"F11.opPattern","COPY",BODY,{"derivedFrom":makeQuery(id+"F10.opPattern","COPY",BODY,{"derivedFrom":makeQuery(id+"F8.opPattern","COPY",BODY,{"derivedFrom":makeQuery(id+"F6.opPattern","COPY",BODY,{"derivedFrom":makeQuery(id+"F5.opPattern","COPY",BODY,{"derivedFrom":makeQuery(id+"F1.opRevolve","SWEPT_BODY",BODY,{"disambiguationData":[OSD([sQuery(id+"F0.wireOp",EDGE,"E1")])]}),"instanceName":"1"}),"instanceName":"1"}),"instanceName":"1"}),"instanceName":"1"}),"instanceName":"1"}),"instanceName":"1"});
            var Q1411;
            Q1411=makeQuery(id+"F12.opPattern","COPY",BODY,{"derivedFrom":makeQuery(id+"F11.opPattern","COPY",BODY,{"derivedFrom":makeQuery(id+"F10.opPattern","COPY",BODY,{"derivedFrom":makeQuery(id+"F8.opPattern","COPY",BODY,{"derivedFrom":makeQuery(id+"F6.opPattern","COPY",BODY,{"derivedFrom":makeQuery(id+"F5.opPattern","COPY",BODY,{"derivedFrom":makeQuery(id+"F2.opPattern","COPY",BODY,{"derivedFrom":makeQuery(id+"F1.opRevolve","SWEPT_BODY",BODY,{"disambiguationData":[OSD([sQuery(id+"F0.wireOp",EDGE,"E1")])]}),"instanceName":"1"}),"instanceName":"1"}),"instanceName":"1"}),"instanceName":"1"}),"instanceName":"1"}),"instanceName":"1"}),"instanceName":"1"});
            var Q1412;
            Q1412=makeQuery(id+"F12.opPattern","COPY",BODY,{"derivedFrom":makeQuery(id+"F11.opPattern","COPY",BODY,{"derivedFrom":makeQuery(id+"F10.opPattern","COPY",BODY,{"derivedFrom":makeQuery(id+"F8.opPattern","COPY",BODY,{"derivedFrom":makeQuery(id+"F6.opPattern","COPY",BODY,{"derivedFrom":makeQuery(id+"F5.opPattern","COPY",BODY,{"derivedFrom":makeQuery(id+"F3.opPattern","COPY",BODY,{"derivedFrom":makeQuery(id+"F2.opPattern","COPY",BODY,{"derivedFrom":makeQuery(id+"F1.opRevolve","SWEPT_BODY",BODY,{"disambiguationData":[OSD([sQuery(id+"F0.wireOp",EDGE,"E1")])]}),"instanceName":"1"}),"instanceName":"1"}),"instanceName":"1"}),"instanceName":"1"}),"instanceName":"1"}),"instanceName":"1"}),"instanceName":"1"}),"instanceName":"1"});
            var Q1413;
            Q1413=makeQuery(id+"F12.opPattern","COPY",BODY,{"derivedFrom":makeQuery(id+"F11.opPattern","COPY",BODY,{"derivedFrom":makeQuery(id+"F10.opPattern","COPY",BODY,{"derivedFrom":makeQuery(id+"F8.opPattern","COPY",BODY,{"derivedFrom":makeQuery(id+"F6.opPattern","COPY",BODY,{"derivedFrom":makeQuery(id+"F5.opPattern","COPY",BODY,{"derivedFrom":makeQuery(id+"F4.opPattern","COPY",BODY,{"derivedFrom":makeQuery(id+"F1.opRevolve","SWEPT_BODY",BODY,{"disambiguationData":[OSD([sQuery(id+"F0.wireOp",EDGE,"E1")])]}),"instanceName":"1"}),"instanceName":"1"}),"instanceName":"1"}),"instanceName":"1"}),"instanceName":"1"}),"instanceName":"1"}),"instanceName":"1"});
            var Q1414;
            Q1414=makeQuery(id+"F12.opPattern","COPY",BODY,{"derivedFrom":makeQuery(id+"F11.opPattern","COPY",BODY,{"derivedFrom":makeQuery(id+"F10.opPattern","COPY",BODY,{"derivedFrom":makeQuery(id+"F8.opPattern","COPY",BODY,{"derivedFrom":makeQuery(id+"F6.opPattern","COPY",BODY,{"derivedFrom":makeQuery(id+"F5.opPattern","COPY",BODY,{"derivedFrom":makeQuery(id+"F4.opPattern","COPY",BODY,{"derivedFrom":makeQuery(id+"F2.opPattern","COPY",BODY,{"derivedFrom":makeQuery(id+"F1.opRevolve","SWEPT_BODY",BODY,{"disambiguationData":[OSD([sQuery(id+"F0.wireOp",EDGE,"E1")])]}),"instanceName":"1"}),"instanceName":"1"}),"instanceName":"1"}),"instanceName":"1"}),"instanceName":"1"}),"instanceName":"1"}),"instanceName":"1"}),"instanceName":"1"});
            var Q1415;
            Q1415=makeQuery(id+"F12.opPattern","COPY",BODY,{"derivedFrom":makeQuery(id+"F11.opPattern","COPY",BODY,{"derivedFrom":makeQuery(id+"F10.opPattern","COPY",BODY,{"derivedFrom":makeQuery(id+"F8.opPattern","COPY",BODY,{"derivedFrom":makeQuery(id+"F6.opPattern","COPY",BODY,{"derivedFrom":makeQuery(id+"F5.opPattern","COPY",BODY,{"derivedFrom":makeQuery(id+"F4.opPattern","COPY",BODY,{"derivedFrom":makeQuery(id+"F3.opPattern","COPY",BODY,{"derivedFrom":makeQuery(id+"F2.opPattern","COPY",BODY,{"derivedFrom":makeQuery(id+"F1.opRevolve","SWEPT_BODY",BODY,{"disambiguationData":[OSD([sQuery(id+"F0.wireOp",EDGE,"E1")])]}),"instanceName":"1"}),"instanceName":"1"}),"instanceName":"1"}),"instanceName":"1"}),"instanceName":"1"}),"instanceName":"1"}),"instanceName":"1"}),"instanceName":"1"}),"instanceName":"1"});
            var Q1416;
            Q1416=makeQuery(id+"F12.opPattern","COPY",BODY,{"derivedFrom":makeQuery(id+"F11.opPattern","COPY",BODY,{"derivedFrom":makeQuery(id+"F10.opPattern","COPY",BODY,{"derivedFrom":makeQuery(id+"F8.opPattern","COPY",BODY,{"derivedFrom":makeQuery(id+"F7.opPattern","COPY",BODY,{"derivedFrom":makeQuery(id+"F1.opRevolve","SWEPT_BODY",BODY,{"disambiguationData":[OSD([sQuery(id+"F0.wireOp",EDGE,"E1")])]}),"instanceName":"1"}),"instanceName":"1"}),"instanceName":"1"}),"instanceName":"1"}),"instanceName":"1"});
            var Q1417;
            Q1417=makeQuery(id+"F12.opPattern","COPY",BODY,{"derivedFrom":makeQuery(id+"F11.opPattern","COPY",BODY,{"derivedFrom":makeQuery(id+"F10.opPattern","COPY",BODY,{"derivedFrom":makeQuery(id+"F8.opPattern","COPY",BODY,{"derivedFrom":makeQuery(id+"F7.opPattern","COPY",BODY,{"derivedFrom":makeQuery(id+"F2.opPattern","COPY",BODY,{"derivedFrom":makeQuery(id+"F1.opRevolve","SWEPT_BODY",BODY,{"disambiguationData":[OSD([sQuery(id+"F0.wireOp",EDGE,"E1")])]}),"instanceName":"1"}),"instanceName":"1"}),"instanceName":"1"}),"instanceName":"1"}),"instanceName":"1"}),"instanceName":"1"});
            var Q1418;
            Q1418=makeQuery(id+"F12.opPattern","COPY",BODY,{"derivedFrom":makeQuery(id+"F11.opPattern","COPY",BODY,{"derivedFrom":makeQuery(id+"F10.opPattern","COPY",BODY,{"derivedFrom":makeQuery(id+"F8.opPattern","COPY",BODY,{"derivedFrom":makeQuery(id+"F7.opPattern","COPY",BODY,{"derivedFrom":makeQuery(id+"F3.opPattern","COPY",BODY,{"derivedFrom":makeQuery(id+"F2.opPattern","COPY",BODY,{"derivedFrom":makeQuery(id+"F1.opRevolve","SWEPT_BODY",BODY,{"disambiguationData":[OSD([sQuery(id+"F0.wireOp",EDGE,"E1")])]}),"instanceName":"1"}),"instanceName":"1"}),"instanceName":"1"}),"instanceName":"1"}),"instanceName":"1"}),"instanceName":"1"}),"instanceName":"1"});
            var Q1419;
            Q1419=makeQuery(id+"F12.opPattern","COPY",BODY,{"derivedFrom":makeQuery(id+"F11.opPattern","COPY",BODY,{"derivedFrom":makeQuery(id+"F10.opPattern","COPY",BODY,{"derivedFrom":makeQuery(id+"F8.opPattern","COPY",BODY,{"derivedFrom":makeQuery(id+"F7.opPattern","COPY",BODY,{"derivedFrom":makeQuery(id+"F4.opPattern","COPY",BODY,{"derivedFrom":makeQuery(id+"F1.opRevolve","SWEPT_BODY",BODY,{"disambiguationData":[OSD([sQuery(id+"F0.wireOp",EDGE,"E1")])]}),"instanceName":"1"}),"instanceName":"1"}),"instanceName":"1"}),"instanceName":"1"}),"instanceName":"1"}),"instanceName":"1"});
            var Q1420;
            Q1420=makeQuery(id+"F12.opPattern","COPY",BODY,{"derivedFrom":makeQuery(id+"F11.opPattern","COPY",BODY,{"derivedFrom":makeQuery(id+"F10.opPattern","COPY",BODY,{"derivedFrom":makeQuery(id+"F8.opPattern","COPY",BODY,{"derivedFrom":makeQuery(id+"F7.opPattern","COPY",BODY,{"derivedFrom":makeQuery(id+"F4.opPattern","COPY",BODY,{"derivedFrom":makeQuery(id+"F2.opPattern","COPY",BODY,{"derivedFrom":makeQuery(id+"F1.opRevolve","SWEPT_BODY",BODY,{"disambiguationData":[OSD([sQuery(id+"F0.wireOp",EDGE,"E1")])]}),"instanceName":"1"}),"instanceName":"1"}),"instanceName":"1"}),"instanceName":"1"}),"instanceName":"1"}),"instanceName":"1"}),"instanceName":"1"});
            var Q1421;
            Q1421=makeQuery(id+"F12.opPattern","COPY",BODY,{"derivedFrom":makeQuery(id+"F11.opPattern","COPY",BODY,{"derivedFrom":makeQuery(id+"F10.opPattern","COPY",BODY,{"derivedFrom":makeQuery(id+"F8.opPattern","COPY",BODY,{"derivedFrom":makeQuery(id+"F7.opPattern","COPY",BODY,{"derivedFrom":makeQuery(id+"F4.opPattern","COPY",BODY,{"derivedFrom":makeQuery(id+"F3.opPattern","COPY",BODY,{"derivedFrom":makeQuery(id+"F2.opPattern","COPY",BODY,{"derivedFrom":makeQuery(id+"F1.opRevolve","SWEPT_BODY",BODY,{"disambiguationData":[OSD([sQuery(id+"F0.wireOp",EDGE,"E1")])]}),"instanceName":"1"}),"instanceName":"1"}),"instanceName":"1"}),"instanceName":"1"}),"instanceName":"1"}),"instanceName":"1"}),"instanceName":"1"}),"instanceName":"1"});
            var Q1422;
            Q1422=makeQuery(id+"F12.opPattern","COPY",BODY,{"derivedFrom":makeQuery(id+"F11.opPattern","COPY",BODY,{"derivedFrom":makeQuery(id+"F10.opPattern","COPY",BODY,{"derivedFrom":makeQuery(id+"F8.opPattern","COPY",BODY,{"derivedFrom":makeQuery(id+"F7.opPattern","COPY",BODY,{"derivedFrom":makeQuery(id+"F5.opPattern","COPY",BODY,{"derivedFrom":makeQuery(id+"F1.opRevolve","SWEPT_BODY",BODY,{"disambiguationData":[OSD([sQuery(id+"F0.wireOp",EDGE,"E1")])]}),"instanceName":"1"}),"instanceName":"1"}),"instanceName":"1"}),"instanceName":"1"}),"instanceName":"1"}),"instanceName":"1"});
            var Q1423;
            Q1423=makeQuery(id+"F12.opPattern","COPY",BODY,{"derivedFrom":makeQuery(id+"F11.opPattern","COPY",BODY,{"derivedFrom":makeQuery(id+"F10.opPattern","COPY",BODY,{"derivedFrom":makeQuery(id+"F8.opPattern","COPY",BODY,{"derivedFrom":makeQuery(id+"F7.opPattern","COPY",BODY,{"derivedFrom":makeQuery(id+"F5.opPattern","COPY",BODY,{"derivedFrom":makeQuery(id+"F2.opPattern","COPY",BODY,{"derivedFrom":makeQuery(id+"F1.opRevolve","SWEPT_BODY",BODY,{"disambiguationData":[OSD([sQuery(id+"F0.wireOp",EDGE,"E1")])]}),"instanceName":"1"}),"instanceName":"1"}),"instanceName":"1"}),"instanceName":"1"}),"instanceName":"1"}),"instanceName":"1"}),"instanceName":"1"});
            var Q1424;
            Q1424=makeQuery(id+"F12.opPattern","COPY",BODY,{"derivedFrom":makeQuery(id+"F11.opPattern","COPY",BODY,{"derivedFrom":makeQuery(id+"F10.opPattern","COPY",BODY,{"derivedFrom":makeQuery(id+"F8.opPattern","COPY",BODY,{"derivedFrom":makeQuery(id+"F7.opPattern","COPY",BODY,{"derivedFrom":makeQuery(id+"F5.opPattern","COPY",BODY,{"derivedFrom":makeQuery(id+"F3.opPattern","COPY",BODY,{"derivedFrom":makeQuery(id+"F2.opPattern","COPY",BODY,{"derivedFrom":makeQuery(id+"F1.opRevolve","SWEPT_BODY",BODY,{"disambiguationData":[OSD([sQuery(id+"F0.wireOp",EDGE,"E1")])]}),"instanceName":"1"}),"instanceName":"1"}),"instanceName":"1"}),"instanceName":"1"}),"instanceName":"1"}),"instanceName":"1"}),"instanceName":"1"}),"instanceName":"1"});
            var Q1425;
            Q1425=makeQuery(id+"F12.opPattern","COPY",BODY,{"derivedFrom":makeQuery(id+"F11.opPattern","COPY",BODY,{"derivedFrom":makeQuery(id+"F10.opPattern","COPY",BODY,{"derivedFrom":makeQuery(id+"F8.opPattern","COPY",BODY,{"derivedFrom":makeQuery(id+"F7.opPattern","COPY",BODY,{"derivedFrom":makeQuery(id+"F5.opPattern","COPY",BODY,{"derivedFrom":makeQuery(id+"F4.opPattern","COPY",BODY,{"derivedFrom":makeQuery(id+"F1.opRevolve","SWEPT_BODY",BODY,{"disambiguationData":[OSD([sQuery(id+"F0.wireOp",EDGE,"E1")])]}),"instanceName":"1"}),"instanceName":"1"}),"instanceName":"1"}),"instanceName":"1"}),"instanceName":"1"}),"instanceName":"1"}),"instanceName":"1"});
            var Q1426;
            Q1426=makeQuery(id+"F12.opPattern","COPY",BODY,{"derivedFrom":makeQuery(id+"F11.opPattern","COPY",BODY,{"derivedFrom":makeQuery(id+"F10.opPattern","COPY",BODY,{"derivedFrom":makeQuery(id+"F8.opPattern","COPY",BODY,{"derivedFrom":makeQuery(id+"F7.opPattern","COPY",BODY,{"derivedFrom":makeQuery(id+"F5.opPattern","COPY",BODY,{"derivedFrom":makeQuery(id+"F4.opPattern","COPY",BODY,{"derivedFrom":makeQuery(id+"F2.opPattern","COPY",BODY,{"derivedFrom":makeQuery(id+"F1.opRevolve","SWEPT_BODY",BODY,{"disambiguationData":[OSD([sQuery(id+"F0.wireOp",EDGE,"E1")])]}),"instanceName":"1"}),"instanceName":"1"}),"instanceName":"1"}),"instanceName":"1"}),"instanceName":"1"}),"instanceName":"1"}),"instanceName":"1"}),"instanceName":"1"});
            var Q1427;
            Q1427=makeQuery(id+"F12.opPattern","COPY",BODY,{"derivedFrom":makeQuery(id+"F11.opPattern","COPY",BODY,{"derivedFrom":makeQuery(id+"F10.opPattern","COPY",BODY,{"derivedFrom":makeQuery(id+"F8.opPattern","COPY",BODY,{"derivedFrom":makeQuery(id+"F7.opPattern","COPY",BODY,{"derivedFrom":makeQuery(id+"F5.opPattern","COPY",BODY,{"derivedFrom":makeQuery(id+"F4.opPattern","COPY",BODY,{"derivedFrom":makeQuery(id+"F3.opPattern","COPY",BODY,{"derivedFrom":makeQuery(id+"F2.opPattern","COPY",BODY,{"derivedFrom":makeQuery(id+"F1.opRevolve","SWEPT_BODY",BODY,{"disambiguationData":[OSD([sQuery(id+"F0.wireOp",EDGE,"E1")])]}),"instanceName":"1"}),"instanceName":"1"}),"instanceName":"1"}),"instanceName":"1"}),"instanceName":"1"}),"instanceName":"1"}),"instanceName":"1"}),"instanceName":"1"}),"instanceName":"1"});
            var Q1428;
            Q1428=makeQuery(id+"F12.opPattern","COPY",BODY,{"derivedFrom":makeQuery(id+"F11.opPattern","COPY",BODY,{"derivedFrom":makeQuery(id+"F10.opPattern","COPY",BODY,{"derivedFrom":makeQuery(id+"F8.opPattern","COPY",BODY,{"derivedFrom":makeQuery(id+"F7.opPattern","COPY",BODY,{"derivedFrom":makeQuery(id+"F6.opPattern","COPY",BODY,{"derivedFrom":makeQuery(id+"F1.opRevolve","SWEPT_BODY",BODY,{"disambiguationData":[OSD([sQuery(id+"F0.wireOp",EDGE,"E1")])]}),"instanceName":"1"}),"instanceName":"1"}),"instanceName":"1"}),"instanceName":"1"}),"instanceName":"1"}),"instanceName":"1"});
            var Q1429;
            Q1429=makeQuery(id+"F12.opPattern","COPY",BODY,{"derivedFrom":makeQuery(id+"F11.opPattern","COPY",BODY,{"derivedFrom":makeQuery(id+"F10.opPattern","COPY",BODY,{"derivedFrom":makeQuery(id+"F8.opPattern","COPY",BODY,{"derivedFrom":makeQuery(id+"F7.opPattern","COPY",BODY,{"derivedFrom":makeQuery(id+"F6.opPattern","COPY",BODY,{"derivedFrom":makeQuery(id+"F2.opPattern","COPY",BODY,{"derivedFrom":makeQuery(id+"F1.opRevolve","SWEPT_BODY",BODY,{"disambiguationData":[OSD([sQuery(id+"F0.wireOp",EDGE,"E1")])]}),"instanceName":"1"}),"instanceName":"1"}),"instanceName":"1"}),"instanceName":"1"}),"instanceName":"1"}),"instanceName":"1"}),"instanceName":"1"});
            var Q1430;
            Q1430=makeQuery(id+"F12.opPattern","COPY",BODY,{"derivedFrom":makeQuery(id+"F11.opPattern","COPY",BODY,{"derivedFrom":makeQuery(id+"F10.opPattern","COPY",BODY,{"derivedFrom":makeQuery(id+"F8.opPattern","COPY",BODY,{"derivedFrom":makeQuery(id+"F7.opPattern","COPY",BODY,{"derivedFrom":makeQuery(id+"F6.opPattern","COPY",BODY,{"derivedFrom":makeQuery(id+"F3.opPattern","COPY",BODY,{"derivedFrom":makeQuery(id+"F2.opPattern","COPY",BODY,{"derivedFrom":makeQuery(id+"F1.opRevolve","SWEPT_BODY",BODY,{"disambiguationData":[OSD([sQuery(id+"F0.wireOp",EDGE,"E1")])]}),"instanceName":"1"}),"instanceName":"1"}),"instanceName":"1"}),"instanceName":"1"}),"instanceName":"1"}),"instanceName":"1"}),"instanceName":"1"}),"instanceName":"1"});
            var Q1431;
            Q1431=makeQuery(id+"F12.opPattern","COPY",BODY,{"derivedFrom":makeQuery(id+"F11.opPattern","COPY",BODY,{"derivedFrom":makeQuery(id+"F10.opPattern","COPY",BODY,{"derivedFrom":makeQuery(id+"F8.opPattern","COPY",BODY,{"derivedFrom":makeQuery(id+"F7.opPattern","COPY",BODY,{"derivedFrom":makeQuery(id+"F6.opPattern","COPY",BODY,{"derivedFrom":makeQuery(id+"F4.opPattern","COPY",BODY,{"derivedFrom":makeQuery(id+"F1.opRevolve","SWEPT_BODY",BODY,{"disambiguationData":[OSD([sQuery(id+"F0.wireOp",EDGE,"E1")])]}),"instanceName":"1"}),"instanceName":"1"}),"instanceName":"1"}),"instanceName":"1"}),"instanceName":"1"}),"instanceName":"1"}),"instanceName":"1"});
            var Q1432;
            Q1432=makeQuery(id+"F12.opPattern","COPY",BODY,{"derivedFrom":makeQuery(id+"F11.opPattern","COPY",BODY,{"derivedFrom":makeQuery(id+"F10.opPattern","COPY",BODY,{"derivedFrom":makeQuery(id+"F8.opPattern","COPY",BODY,{"derivedFrom":makeQuery(id+"F7.opPattern","COPY",BODY,{"derivedFrom":makeQuery(id+"F6.opPattern","COPY",BODY,{"derivedFrom":makeQuery(id+"F4.opPattern","COPY",BODY,{"derivedFrom":makeQuery(id+"F2.opPattern","COPY",BODY,{"derivedFrom":makeQuery(id+"F1.opRevolve","SWEPT_BODY",BODY,{"disambiguationData":[OSD([sQuery(id+"F0.wireOp",EDGE,"E1")])]}),"instanceName":"1"}),"instanceName":"1"}),"instanceName":"1"}),"instanceName":"1"}),"instanceName":"1"}),"instanceName":"1"}),"instanceName":"1"}),"instanceName":"1"});
            var Q1433;
            Q1433=makeQuery(id+"F12.opPattern","COPY",BODY,{"derivedFrom":makeQuery(id+"F11.opPattern","COPY",BODY,{"derivedFrom":makeQuery(id+"F10.opPattern","COPY",BODY,{"derivedFrom":makeQuery(id+"F8.opPattern","COPY",BODY,{"derivedFrom":makeQuery(id+"F7.opPattern","COPY",BODY,{"derivedFrom":makeQuery(id+"F6.opPattern","COPY",BODY,{"derivedFrom":makeQuery(id+"F4.opPattern","COPY",BODY,{"derivedFrom":makeQuery(id+"F3.opPattern","COPY",BODY,{"derivedFrom":makeQuery(id+"F2.opPattern","COPY",BODY,{"derivedFrom":makeQuery(id+"F1.opRevolve","SWEPT_BODY",BODY,{"disambiguationData":[OSD([sQuery(id+"F0.wireOp",EDGE,"E1")])]}),"instanceName":"1"}),"instanceName":"1"}),"instanceName":"1"}),"instanceName":"1"}),"instanceName":"1"}),"instanceName":"1"}),"instanceName":"1"}),"instanceName":"1"}),"instanceName":"1"});
            var Q1434;
            Q1434=makeQuery(id+"F12.opPattern","COPY",BODY,{"derivedFrom":makeQuery(id+"F11.opPattern","COPY",BODY,{"derivedFrom":makeQuery(id+"F10.opPattern","COPY",BODY,{"derivedFrom":makeQuery(id+"F8.opPattern","COPY",BODY,{"derivedFrom":makeQuery(id+"F7.opPattern","COPY",BODY,{"derivedFrom":makeQuery(id+"F6.opPattern","COPY",BODY,{"derivedFrom":makeQuery(id+"F5.opPattern","COPY",BODY,{"derivedFrom":makeQuery(id+"F1.opRevolve","SWEPT_BODY",BODY,{"disambiguationData":[OSD([sQuery(id+"F0.wireOp",EDGE,"E1")])]}),"instanceName":"1"}),"instanceName":"1"}),"instanceName":"1"}),"instanceName":"1"}),"instanceName":"1"}),"instanceName":"1"}),"instanceName":"1"});
            var Q1435;
            Q1435=makeQuery(id+"F12.opPattern","COPY",BODY,{"derivedFrom":makeQuery(id+"F11.opPattern","COPY",BODY,{"derivedFrom":makeQuery(id+"F10.opPattern","COPY",BODY,{"derivedFrom":makeQuery(id+"F8.opPattern","COPY",BODY,{"derivedFrom":makeQuery(id+"F7.opPattern","COPY",BODY,{"derivedFrom":makeQuery(id+"F6.opPattern","COPY",BODY,{"derivedFrom":makeQuery(id+"F5.opPattern","COPY",BODY,{"derivedFrom":makeQuery(id+"F2.opPattern","COPY",BODY,{"derivedFrom":makeQuery(id+"F1.opRevolve","SWEPT_BODY",BODY,{"disambiguationData":[OSD([sQuery(id+"F0.wireOp",EDGE,"E1")])]}),"instanceName":"1"}),"instanceName":"1"}),"instanceName":"1"}),"instanceName":"1"}),"instanceName":"1"}),"instanceName":"1"}),"instanceName":"1"}),"instanceName":"1"});
            var Q1436;
            Q1436=makeQuery(id+"F12.opPattern","COPY",BODY,{"derivedFrom":makeQuery(id+"F11.opPattern","COPY",BODY,{"derivedFrom":makeQuery(id+"F10.opPattern","COPY",BODY,{"derivedFrom":makeQuery(id+"F8.opPattern","COPY",BODY,{"derivedFrom":makeQuery(id+"F7.opPattern","COPY",BODY,{"derivedFrom":makeQuery(id+"F6.opPattern","COPY",BODY,{"derivedFrom":makeQuery(id+"F5.opPattern","COPY",BODY,{"derivedFrom":makeQuery(id+"F3.opPattern","COPY",BODY,{"derivedFrom":makeQuery(id+"F2.opPattern","COPY",BODY,{"derivedFrom":makeQuery(id+"F1.opRevolve","SWEPT_BODY",BODY,{"disambiguationData":[OSD([sQuery(id+"F0.wireOp",EDGE,"E1")])]}),"instanceName":"1"}),"instanceName":"1"}),"instanceName":"1"}),"instanceName":"1"}),"instanceName":"1"}),"instanceName":"1"}),"instanceName":"1"}),"instanceName":"1"}),"instanceName":"1"});
            var Q1437;
            Q1437=makeQuery(id+"F12.opPattern","COPY",BODY,{"derivedFrom":makeQuery(id+"F11.opPattern","COPY",BODY,{"derivedFrom":makeQuery(id+"F10.opPattern","COPY",BODY,{"derivedFrom":makeQuery(id+"F8.opPattern","COPY",BODY,{"derivedFrom":makeQuery(id+"F7.opPattern","COPY",BODY,{"derivedFrom":makeQuery(id+"F6.opPattern","COPY",BODY,{"derivedFrom":makeQuery(id+"F5.opPattern","COPY",BODY,{"derivedFrom":makeQuery(id+"F4.opPattern","COPY",BODY,{"derivedFrom":makeQuery(id+"F1.opRevolve","SWEPT_BODY",BODY,{"disambiguationData":[OSD([sQuery(id+"F0.wireOp",EDGE,"E1")])]}),"instanceName":"1"}),"instanceName":"1"}),"instanceName":"1"}),"instanceName":"1"}),"instanceName":"1"}),"instanceName":"1"}),"instanceName":"1"}),"instanceName":"1"});
            var Q1438;
            Q1438=makeQuery(id+"F12.opPattern","COPY",BODY,{"derivedFrom":makeQuery(id+"F11.opPattern","COPY",BODY,{"derivedFrom":makeQuery(id+"F10.opPattern","COPY",BODY,{"derivedFrom":makeQuery(id+"F8.opPattern","COPY",BODY,{"derivedFrom":makeQuery(id+"F7.opPattern","COPY",BODY,{"derivedFrom":makeQuery(id+"F6.opPattern","COPY",BODY,{"derivedFrom":makeQuery(id+"F5.opPattern","COPY",BODY,{"derivedFrom":makeQuery(id+"F4.opPattern","COPY",BODY,{"derivedFrom":makeQuery(id+"F2.opPattern","COPY",BODY,{"derivedFrom":makeQuery(id+"F1.opRevolve","SWEPT_BODY",BODY,{"disambiguationData":[OSD([sQuery(id+"F0.wireOp",EDGE,"E1")])]}),"instanceName":"1"}),"instanceName":"1"}),"instanceName":"1"}),"instanceName":"1"}),"instanceName":"1"}),"instanceName":"1"}),"instanceName":"1"}),"instanceName":"1"}),"instanceName":"1"});
            var Q1439;
            Q1439=makeQuery(id+"F12.opPattern","COPY",BODY,{"derivedFrom":makeQuery(id+"F11.opPattern","COPY",BODY,{"derivedFrom":makeQuery(id+"F10.opPattern","COPY",BODY,{"derivedFrom":makeQuery(id+"F8.opPattern","COPY",BODY,{"derivedFrom":makeQuery(id+"F7.opPattern","COPY",BODY,{"derivedFrom":makeQuery(id+"F6.opPattern","COPY",BODY,{"derivedFrom":makeQuery(id+"F5.opPattern","COPY",BODY,{"derivedFrom":makeQuery(id+"F4.opPattern","COPY",BODY,{"derivedFrom":makeQuery(id+"F3.opPattern","COPY",BODY,{"derivedFrom":makeQuery(id+"F2.opPattern","COPY",BODY,{"derivedFrom":makeQuery(id+"F1.opRevolve","SWEPT_BODY",BODY,{"disambiguationData":[OSD([sQuery(id+"F0.wireOp",EDGE,"E1")])]}),"instanceName":"1"}),"instanceName":"1"}),"instanceName":"1"}),"instanceName":"1"}),"instanceName":"1"}),"instanceName":"1"}),"instanceName":"1"}),"instanceName":"1"}),"instanceName":"1"}),"instanceName":"1"});
            var Q1440;
            Q1440=makeQuery(id+"F12.opPattern","COPY",BODY,{"derivedFrom":makeQuery(id+"F11.opPattern","COPY",BODY,{"derivedFrom":makeQuery(id+"F10.opPattern","COPY",BODY,{"derivedFrom":makeQuery(id+"F9.opPattern","COPY",BODY,{"derivedFrom":makeQuery(id+"F1.opRevolve","SWEPT_BODY",BODY,{"disambiguationData":[OSD([sQuery(id+"F0.wireOp",EDGE,"E1")])]}),"instanceName":"1"}),"instanceName":"1"}),"instanceName":"1"}),"instanceName":"1"});
            var Q1441;
            Q1441=makeQuery(id+"F12.opPattern","COPY",BODY,{"derivedFrom":makeQuery(id+"F11.opPattern","COPY",BODY,{"derivedFrom":makeQuery(id+"F10.opPattern","COPY",BODY,{"derivedFrom":makeQuery(id+"F9.opPattern","COPY",BODY,{"derivedFrom":makeQuery(id+"F2.opPattern","COPY",BODY,{"derivedFrom":makeQuery(id+"F1.opRevolve","SWEPT_BODY",BODY,{"disambiguationData":[OSD([sQuery(id+"F0.wireOp",EDGE,"E1")])]}),"instanceName":"1"}),"instanceName":"1"}),"instanceName":"1"}),"instanceName":"1"}),"instanceName":"1"});
            var Q1442;
            Q1442=makeQuery(id+"F12.opPattern","COPY",BODY,{"derivedFrom":makeQuery(id+"F11.opPattern","COPY",BODY,{"derivedFrom":makeQuery(id+"F10.opPattern","COPY",BODY,{"derivedFrom":makeQuery(id+"F9.opPattern","COPY",BODY,{"derivedFrom":makeQuery(id+"F3.opPattern","COPY",BODY,{"derivedFrom":makeQuery(id+"F2.opPattern","COPY",BODY,{"derivedFrom":makeQuery(id+"F1.opRevolve","SWEPT_BODY",BODY,{"disambiguationData":[OSD([sQuery(id+"F0.wireOp",EDGE,"E1")])]}),"instanceName":"1"}),"instanceName":"1"}),"instanceName":"1"}),"instanceName":"1"}),"instanceName":"1"}),"instanceName":"1"});
            var Q1443;
            Q1443=makeQuery(id+"F12.opPattern","COPY",BODY,{"derivedFrom":makeQuery(id+"F11.opPattern","COPY",BODY,{"derivedFrom":makeQuery(id+"F10.opPattern","COPY",BODY,{"derivedFrom":makeQuery(id+"F9.opPattern","COPY",BODY,{"derivedFrom":makeQuery(id+"F4.opPattern","COPY",BODY,{"derivedFrom":makeQuery(id+"F1.opRevolve","SWEPT_BODY",BODY,{"disambiguationData":[OSD([sQuery(id+"F0.wireOp",EDGE,"E1")])]}),"instanceName":"1"}),"instanceName":"1"}),"instanceName":"1"}),"instanceName":"1"}),"instanceName":"1"});
            var Q1444;
            Q1444=makeQuery(id+"F12.opPattern","COPY",BODY,{"derivedFrom":makeQuery(id+"F11.opPattern","COPY",BODY,{"derivedFrom":makeQuery(id+"F10.opPattern","COPY",BODY,{"derivedFrom":makeQuery(id+"F9.opPattern","COPY",BODY,{"derivedFrom":makeQuery(id+"F4.opPattern","COPY",BODY,{"derivedFrom":makeQuery(id+"F2.opPattern","COPY",BODY,{"derivedFrom":makeQuery(id+"F1.opRevolve","SWEPT_BODY",BODY,{"disambiguationData":[OSD([sQuery(id+"F0.wireOp",EDGE,"E1")])]}),"instanceName":"1"}),"instanceName":"1"}),"instanceName":"1"}),"instanceName":"1"}),"instanceName":"1"}),"instanceName":"1"});
            var Q1445;
            Q1445=makeQuery(id+"F12.opPattern","COPY",BODY,{"derivedFrom":makeQuery(id+"F11.opPattern","COPY",BODY,{"derivedFrom":makeQuery(id+"F10.opPattern","COPY",BODY,{"derivedFrom":makeQuery(id+"F9.opPattern","COPY",BODY,{"derivedFrom":makeQuery(id+"F4.opPattern","COPY",BODY,{"derivedFrom":makeQuery(id+"F3.opPattern","COPY",BODY,{"derivedFrom":makeQuery(id+"F2.opPattern","COPY",BODY,{"derivedFrom":makeQuery(id+"F1.opRevolve","SWEPT_BODY",BODY,{"disambiguationData":[OSD([sQuery(id+"F0.wireOp",EDGE,"E1")])]}),"instanceName":"1"}),"instanceName":"1"}),"instanceName":"1"}),"instanceName":"1"}),"instanceName":"1"}),"instanceName":"1"}),"instanceName":"1"});
            var Q1446;
            Q1446=makeQuery(id+"F12.opPattern","COPY",BODY,{"derivedFrom":makeQuery(id+"F11.opPattern","COPY",BODY,{"derivedFrom":makeQuery(id+"F10.opPattern","COPY",BODY,{"derivedFrom":makeQuery(id+"F9.opPattern","COPY",BODY,{"derivedFrom":makeQuery(id+"F5.opPattern","COPY",BODY,{"derivedFrom":makeQuery(id+"F1.opRevolve","SWEPT_BODY",BODY,{"disambiguationData":[OSD([sQuery(id+"F0.wireOp",EDGE,"E1")])]}),"instanceName":"1"}),"instanceName":"1"}),"instanceName":"1"}),"instanceName":"1"}),"instanceName":"1"});
            var Q1447;
            Q1447=makeQuery(id+"F12.opPattern","COPY",BODY,{"derivedFrom":makeQuery(id+"F11.opPattern","COPY",BODY,{"derivedFrom":makeQuery(id+"F10.opPattern","COPY",BODY,{"derivedFrom":makeQuery(id+"F9.opPattern","COPY",BODY,{"derivedFrom":makeQuery(id+"F5.opPattern","COPY",BODY,{"derivedFrom":makeQuery(id+"F2.opPattern","COPY",BODY,{"derivedFrom":makeQuery(id+"F1.opRevolve","SWEPT_BODY",BODY,{"disambiguationData":[OSD([sQuery(id+"F0.wireOp",EDGE,"E1")])]}),"instanceName":"1"}),"instanceName":"1"}),"instanceName":"1"}),"instanceName":"1"}),"instanceName":"1"}),"instanceName":"1"});
            var Q1448;
            Q1448=makeQuery(id+"F12.opPattern","COPY",BODY,{"derivedFrom":makeQuery(id+"F11.opPattern","COPY",BODY,{"derivedFrom":makeQuery(id+"F10.opPattern","COPY",BODY,{"derivedFrom":makeQuery(id+"F9.opPattern","COPY",BODY,{"derivedFrom":makeQuery(id+"F5.opPattern","COPY",BODY,{"derivedFrom":makeQuery(id+"F3.opPattern","COPY",BODY,{"derivedFrom":makeQuery(id+"F2.opPattern","COPY",BODY,{"derivedFrom":makeQuery(id+"F1.opRevolve","SWEPT_BODY",BODY,{"disambiguationData":[OSD([sQuery(id+"F0.wireOp",EDGE,"E1")])]}),"instanceName":"1"}),"instanceName":"1"}),"instanceName":"1"}),"instanceName":"1"}),"instanceName":"1"}),"instanceName":"1"}),"instanceName":"1"});
            var Q1449;
            Q1449=makeQuery(id+"F12.opPattern","COPY",BODY,{"derivedFrom":makeQuery(id+"F11.opPattern","COPY",BODY,{"derivedFrom":makeQuery(id+"F10.opPattern","COPY",BODY,{"derivedFrom":makeQuery(id+"F9.opPattern","COPY",BODY,{"derivedFrom":makeQuery(id+"F5.opPattern","COPY",BODY,{"derivedFrom":makeQuery(id+"F4.opPattern","COPY",BODY,{"derivedFrom":makeQuery(id+"F1.opRevolve","SWEPT_BODY",BODY,{"disambiguationData":[OSD([sQuery(id+"F0.wireOp",EDGE,"E1")])]}),"instanceName":"1"}),"instanceName":"1"}),"instanceName":"1"}),"instanceName":"1"}),"instanceName":"1"}),"instanceName":"1"});
            var Q1450;
            Q1450=makeQuery(id+"F12.opPattern","COPY",BODY,{"derivedFrom":makeQuery(id+"F11.opPattern","COPY",BODY,{"derivedFrom":makeQuery(id+"F10.opPattern","COPY",BODY,{"derivedFrom":makeQuery(id+"F9.opPattern","COPY",BODY,{"derivedFrom":makeQuery(id+"F5.opPattern","COPY",BODY,{"derivedFrom":makeQuery(id+"F4.opPattern","COPY",BODY,{"derivedFrom":makeQuery(id+"F2.opPattern","COPY",BODY,{"derivedFrom":makeQuery(id+"F1.opRevolve","SWEPT_BODY",BODY,{"disambiguationData":[OSD([sQuery(id+"F0.wireOp",EDGE,"E1")])]}),"instanceName":"1"}),"instanceName":"1"}),"instanceName":"1"}),"instanceName":"1"}),"instanceName":"1"}),"instanceName":"1"}),"instanceName":"1"});
            var Q1451;
            Q1451=makeQuery(id+"F12.opPattern","COPY",BODY,{"derivedFrom":makeQuery(id+"F11.opPattern","COPY",BODY,{"derivedFrom":makeQuery(id+"F10.opPattern","COPY",BODY,{"derivedFrom":makeQuery(id+"F9.opPattern","COPY",BODY,{"derivedFrom":makeQuery(id+"F5.opPattern","COPY",BODY,{"derivedFrom":makeQuery(id+"F4.opPattern","COPY",BODY,{"derivedFrom":makeQuery(id+"F3.opPattern","COPY",BODY,{"derivedFrom":makeQuery(id+"F2.opPattern","COPY",BODY,{"derivedFrom":makeQuery(id+"F1.opRevolve","SWEPT_BODY",BODY,{"disambiguationData":[OSD([sQuery(id+"F0.wireOp",EDGE,"E1")])]}),"instanceName":"1"}),"instanceName":"1"}),"instanceName":"1"}),"instanceName":"1"}),"instanceName":"1"}),"instanceName":"1"}),"instanceName":"1"}),"instanceName":"1"});
            var Q1452;
            Q1452=makeQuery(id+"F12.opPattern","COPY",BODY,{"derivedFrom":makeQuery(id+"F11.opPattern","COPY",BODY,{"derivedFrom":makeQuery(id+"F10.opPattern","COPY",BODY,{"derivedFrom":makeQuery(id+"F9.opPattern","COPY",BODY,{"derivedFrom":makeQuery(id+"F6.opPattern","COPY",BODY,{"derivedFrom":makeQuery(id+"F1.opRevolve","SWEPT_BODY",BODY,{"disambiguationData":[OSD([sQuery(id+"F0.wireOp",EDGE,"E1")])]}),"instanceName":"1"}),"instanceName":"1"}),"instanceName":"1"}),"instanceName":"1"}),"instanceName":"1"});
            var Q1453;
            Q1453=makeQuery(id+"F12.opPattern","COPY",BODY,{"derivedFrom":makeQuery(id+"F11.opPattern","COPY",BODY,{"derivedFrom":makeQuery(id+"F10.opPattern","COPY",BODY,{"derivedFrom":makeQuery(id+"F9.opPattern","COPY",BODY,{"derivedFrom":makeQuery(id+"F6.opPattern","COPY",BODY,{"derivedFrom":makeQuery(id+"F2.opPattern","COPY",BODY,{"derivedFrom":makeQuery(id+"F1.opRevolve","SWEPT_BODY",BODY,{"disambiguationData":[OSD([sQuery(id+"F0.wireOp",EDGE,"E1")])]}),"instanceName":"1"}),"instanceName":"1"}),"instanceName":"1"}),"instanceName":"1"}),"instanceName":"1"}),"instanceName":"1"});
            var Q1454;
            Q1454=makeQuery(id+"F12.opPattern","COPY",BODY,{"derivedFrom":makeQuery(id+"F11.opPattern","COPY",BODY,{"derivedFrom":makeQuery(id+"F10.opPattern","COPY",BODY,{"derivedFrom":makeQuery(id+"F9.opPattern","COPY",BODY,{"derivedFrom":makeQuery(id+"F6.opPattern","COPY",BODY,{"derivedFrom":makeQuery(id+"F3.opPattern","COPY",BODY,{"derivedFrom":makeQuery(id+"F2.opPattern","COPY",BODY,{"derivedFrom":makeQuery(id+"F1.opRevolve","SWEPT_BODY",BODY,{"disambiguationData":[OSD([sQuery(id+"F0.wireOp",EDGE,"E1")])]}),"instanceName":"1"}),"instanceName":"1"}),"instanceName":"1"}),"instanceName":"1"}),"instanceName":"1"}),"instanceName":"1"}),"instanceName":"1"});
            var Q1455;
            Q1455=makeQuery(id+"F12.opPattern","COPY",BODY,{"derivedFrom":makeQuery(id+"F11.opPattern","COPY",BODY,{"derivedFrom":makeQuery(id+"F10.opPattern","COPY",BODY,{"derivedFrom":makeQuery(id+"F9.opPattern","COPY",BODY,{"derivedFrom":makeQuery(id+"F6.opPattern","COPY",BODY,{"derivedFrom":makeQuery(id+"F4.opPattern","COPY",BODY,{"derivedFrom":makeQuery(id+"F1.opRevolve","SWEPT_BODY",BODY,{"disambiguationData":[OSD([sQuery(id+"F0.wireOp",EDGE,"E1")])]}),"instanceName":"1"}),"instanceName":"1"}),"instanceName":"1"}),"instanceName":"1"}),"instanceName":"1"}),"instanceName":"1"});
            var Q1456;
            Q1456=makeQuery(id+"F12.opPattern","COPY",BODY,{"derivedFrom":makeQuery(id+"F11.opPattern","COPY",BODY,{"derivedFrom":makeQuery(id+"F10.opPattern","COPY",BODY,{"derivedFrom":makeQuery(id+"F9.opPattern","COPY",BODY,{"derivedFrom":makeQuery(id+"F6.opPattern","COPY",BODY,{"derivedFrom":makeQuery(id+"F4.opPattern","COPY",BODY,{"derivedFrom":makeQuery(id+"F2.opPattern","COPY",BODY,{"derivedFrom":makeQuery(id+"F1.opRevolve","SWEPT_BODY",BODY,{"disambiguationData":[OSD([sQuery(id+"F0.wireOp",EDGE,"E1")])]}),"instanceName":"1"}),"instanceName":"1"}),"instanceName":"1"}),"instanceName":"1"}),"instanceName":"1"}),"instanceName":"1"}),"instanceName":"1"});
            var Q1457;
            Q1457=makeQuery(id+"F12.opPattern","COPY",BODY,{"derivedFrom":makeQuery(id+"F11.opPattern","COPY",BODY,{"derivedFrom":makeQuery(id+"F10.opPattern","COPY",BODY,{"derivedFrom":makeQuery(id+"F9.opPattern","COPY",BODY,{"derivedFrom":makeQuery(id+"F6.opPattern","COPY",BODY,{"derivedFrom":makeQuery(id+"F4.opPattern","COPY",BODY,{"derivedFrom":makeQuery(id+"F3.opPattern","COPY",BODY,{"derivedFrom":makeQuery(id+"F2.opPattern","COPY",BODY,{"derivedFrom":makeQuery(id+"F1.opRevolve","SWEPT_BODY",BODY,{"disambiguationData":[OSD([sQuery(id+"F0.wireOp",EDGE,"E1")])]}),"instanceName":"1"}),"instanceName":"1"}),"instanceName":"1"}),"instanceName":"1"}),"instanceName":"1"}),"instanceName":"1"}),"instanceName":"1"}),"instanceName":"1"});
            var Q1458;
            Q1458=makeQuery(id+"F12.opPattern","COPY",BODY,{"derivedFrom":makeQuery(id+"F11.opPattern","COPY",BODY,{"derivedFrom":makeQuery(id+"F10.opPattern","COPY",BODY,{"derivedFrom":makeQuery(id+"F9.opPattern","COPY",BODY,{"derivedFrom":makeQuery(id+"F6.opPattern","COPY",BODY,{"derivedFrom":makeQuery(id+"F5.opPattern","COPY",BODY,{"derivedFrom":makeQuery(id+"F1.opRevolve","SWEPT_BODY",BODY,{"disambiguationData":[OSD([sQuery(id+"F0.wireOp",EDGE,"E1")])]}),"instanceName":"1"}),"instanceName":"1"}),"instanceName":"1"}),"instanceName":"1"}),"instanceName":"1"}),"instanceName":"1"});
            var Q1459;
            Q1459=makeQuery(id+"F12.opPattern","COPY",BODY,{"derivedFrom":makeQuery(id+"F11.opPattern","COPY",BODY,{"derivedFrom":makeQuery(id+"F10.opPattern","COPY",BODY,{"derivedFrom":makeQuery(id+"F9.opPattern","COPY",BODY,{"derivedFrom":makeQuery(id+"F6.opPattern","COPY",BODY,{"derivedFrom":makeQuery(id+"F5.opPattern","COPY",BODY,{"derivedFrom":makeQuery(id+"F2.opPattern","COPY",BODY,{"derivedFrom":makeQuery(id+"F1.opRevolve","SWEPT_BODY",BODY,{"disambiguationData":[OSD([sQuery(id+"F0.wireOp",EDGE,"E1")])]}),"instanceName":"1"}),"instanceName":"1"}),"instanceName":"1"}),"instanceName":"1"}),"instanceName":"1"}),"instanceName":"1"}),"instanceName":"1"});
            var Q1460;
            Q1460=makeQuery(id+"F12.opPattern","COPY",BODY,{"derivedFrom":makeQuery(id+"F11.opPattern","COPY",BODY,{"derivedFrom":makeQuery(id+"F10.opPattern","COPY",BODY,{"derivedFrom":makeQuery(id+"F9.opPattern","COPY",BODY,{"derivedFrom":makeQuery(id+"F6.opPattern","COPY",BODY,{"derivedFrom":makeQuery(id+"F5.opPattern","COPY",BODY,{"derivedFrom":makeQuery(id+"F3.opPattern","COPY",BODY,{"derivedFrom":makeQuery(id+"F2.opPattern","COPY",BODY,{"derivedFrom":makeQuery(id+"F1.opRevolve","SWEPT_BODY",BODY,{"disambiguationData":[OSD([sQuery(id+"F0.wireOp",EDGE,"E1")])]}),"instanceName":"1"}),"instanceName":"1"}),"instanceName":"1"}),"instanceName":"1"}),"instanceName":"1"}),"instanceName":"1"}),"instanceName":"1"}),"instanceName":"1"});
            var Q1461;
            Q1461=makeQuery(id+"F12.opPattern","COPY",BODY,{"derivedFrom":makeQuery(id+"F11.opPattern","COPY",BODY,{"derivedFrom":makeQuery(id+"F10.opPattern","COPY",BODY,{"derivedFrom":makeQuery(id+"F9.opPattern","COPY",BODY,{"derivedFrom":makeQuery(id+"F6.opPattern","COPY",BODY,{"derivedFrom":makeQuery(id+"F5.opPattern","COPY",BODY,{"derivedFrom":makeQuery(id+"F4.opPattern","COPY",BODY,{"derivedFrom":makeQuery(id+"F1.opRevolve","SWEPT_BODY",BODY,{"disambiguationData":[OSD([sQuery(id+"F0.wireOp",EDGE,"E1")])]}),"instanceName":"1"}),"instanceName":"1"}),"instanceName":"1"}),"instanceName":"1"}),"instanceName":"1"}),"instanceName":"1"}),"instanceName":"1"});
            var Q1462;
            Q1462=makeQuery(id+"F12.opPattern","COPY",BODY,{"derivedFrom":makeQuery(id+"F11.opPattern","COPY",BODY,{"derivedFrom":makeQuery(id+"F10.opPattern","COPY",BODY,{"derivedFrom":makeQuery(id+"F9.opPattern","COPY",BODY,{"derivedFrom":makeQuery(id+"F6.opPattern","COPY",BODY,{"derivedFrom":makeQuery(id+"F5.opPattern","COPY",BODY,{"derivedFrom":makeQuery(id+"F4.opPattern","COPY",BODY,{"derivedFrom":makeQuery(id+"F2.opPattern","COPY",BODY,{"derivedFrom":makeQuery(id+"F1.opRevolve","SWEPT_BODY",BODY,{"disambiguationData":[OSD([sQuery(id+"F0.wireOp",EDGE,"E1")])]}),"instanceName":"1"}),"instanceName":"1"}),"instanceName":"1"}),"instanceName":"1"}),"instanceName":"1"}),"instanceName":"1"}),"instanceName":"1"}),"instanceName":"1"});
            var Q1463;
            Q1463=makeQuery(id+"F12.opPattern","COPY",BODY,{"derivedFrom":makeQuery(id+"F11.opPattern","COPY",BODY,{"derivedFrom":makeQuery(id+"F10.opPattern","COPY",BODY,{"derivedFrom":makeQuery(id+"F9.opPattern","COPY",BODY,{"derivedFrom":makeQuery(id+"F6.opPattern","COPY",BODY,{"derivedFrom":makeQuery(id+"F5.opPattern","COPY",BODY,{"derivedFrom":makeQuery(id+"F4.opPattern","COPY",BODY,{"derivedFrom":makeQuery(id+"F3.opPattern","COPY",BODY,{"derivedFrom":makeQuery(id+"F2.opPattern","COPY",BODY,{"derivedFrom":makeQuery(id+"F1.opRevolve","SWEPT_BODY",BODY,{"disambiguationData":[OSD([sQuery(id+"F0.wireOp",EDGE,"E1")])]}),"instanceName":"1"}),"instanceName":"1"}),"instanceName":"1"}),"instanceName":"1"}),"instanceName":"1"}),"instanceName":"1"}),"instanceName":"1"}),"instanceName":"1"}),"instanceName":"1"});
            var Q1464;
            Q1464=makeQuery(id+"F12.opPattern","COPY",BODY,{"derivedFrom":makeQuery(id+"F11.opPattern","COPY",BODY,{"derivedFrom":makeQuery(id+"F10.opPattern","COPY",BODY,{"derivedFrom":makeQuery(id+"F9.opPattern","COPY",BODY,{"derivedFrom":makeQuery(id+"F7.opPattern","COPY",BODY,{"derivedFrom":makeQuery(id+"F1.opRevolve","SWEPT_BODY",BODY,{"disambiguationData":[OSD([sQuery(id+"F0.wireOp",EDGE,"E1")])]}),"instanceName":"1"}),"instanceName":"1"}),"instanceName":"1"}),"instanceName":"1"}),"instanceName":"1"});
            var Q1465;
            Q1465=makeQuery(id+"F12.opPattern","COPY",BODY,{"derivedFrom":makeQuery(id+"F11.opPattern","COPY",BODY,{"derivedFrom":makeQuery(id+"F10.opPattern","COPY",BODY,{"derivedFrom":makeQuery(id+"F9.opPattern","COPY",BODY,{"derivedFrom":makeQuery(id+"F7.opPattern","COPY",BODY,{"derivedFrom":makeQuery(id+"F2.opPattern","COPY",BODY,{"derivedFrom":makeQuery(id+"F1.opRevolve","SWEPT_BODY",BODY,{"disambiguationData":[OSD([sQuery(id+"F0.wireOp",EDGE,"E1")])]}),"instanceName":"1"}),"instanceName":"1"}),"instanceName":"1"}),"instanceName":"1"}),"instanceName":"1"}),"instanceName":"1"});
            var Q1466;
            Q1466=makeQuery(id+"F12.opPattern","COPY",BODY,{"derivedFrom":makeQuery(id+"F11.opPattern","COPY",BODY,{"derivedFrom":makeQuery(id+"F10.opPattern","COPY",BODY,{"derivedFrom":makeQuery(id+"F9.opPattern","COPY",BODY,{"derivedFrom":makeQuery(id+"F7.opPattern","COPY",BODY,{"derivedFrom":makeQuery(id+"F3.opPattern","COPY",BODY,{"derivedFrom":makeQuery(id+"F2.opPattern","COPY",BODY,{"derivedFrom":makeQuery(id+"F1.opRevolve","SWEPT_BODY",BODY,{"disambiguationData":[OSD([sQuery(id+"F0.wireOp",EDGE,"E1")])]}),"instanceName":"1"}),"instanceName":"1"}),"instanceName":"1"}),"instanceName":"1"}),"instanceName":"1"}),"instanceName":"1"}),"instanceName":"1"});
            var Q1467;
            Q1467=makeQuery(id+"F12.opPattern","COPY",BODY,{"derivedFrom":makeQuery(id+"F11.opPattern","COPY",BODY,{"derivedFrom":makeQuery(id+"F10.opPattern","COPY",BODY,{"derivedFrom":makeQuery(id+"F9.opPattern","COPY",BODY,{"derivedFrom":makeQuery(id+"F7.opPattern","COPY",BODY,{"derivedFrom":makeQuery(id+"F4.opPattern","COPY",BODY,{"derivedFrom":makeQuery(id+"F1.opRevolve","SWEPT_BODY",BODY,{"disambiguationData":[OSD([sQuery(id+"F0.wireOp",EDGE,"E1")])]}),"instanceName":"1"}),"instanceName":"1"}),"instanceName":"1"}),"instanceName":"1"}),"instanceName":"1"}),"instanceName":"1"});
            var Q1468;
            Q1468=makeQuery(id+"F12.opPattern","COPY",BODY,{"derivedFrom":makeQuery(id+"F11.opPattern","COPY",BODY,{"derivedFrom":makeQuery(id+"F10.opPattern","COPY",BODY,{"derivedFrom":makeQuery(id+"F9.opPattern","COPY",BODY,{"derivedFrom":makeQuery(id+"F7.opPattern","COPY",BODY,{"derivedFrom":makeQuery(id+"F4.opPattern","COPY",BODY,{"derivedFrom":makeQuery(id+"F2.opPattern","COPY",BODY,{"derivedFrom":makeQuery(id+"F1.opRevolve","SWEPT_BODY",BODY,{"disambiguationData":[OSD([sQuery(id+"F0.wireOp",EDGE,"E1")])]}),"instanceName":"1"}),"instanceName":"1"}),"instanceName":"1"}),"instanceName":"1"}),"instanceName":"1"}),"instanceName":"1"}),"instanceName":"1"});
            var Q1469;
            Q1469=makeQuery(id+"F12.opPattern","COPY",BODY,{"derivedFrom":makeQuery(id+"F11.opPattern","COPY",BODY,{"derivedFrom":makeQuery(id+"F10.opPattern","COPY",BODY,{"derivedFrom":makeQuery(id+"F9.opPattern","COPY",BODY,{"derivedFrom":makeQuery(id+"F7.opPattern","COPY",BODY,{"derivedFrom":makeQuery(id+"F4.opPattern","COPY",BODY,{"derivedFrom":makeQuery(id+"F3.opPattern","COPY",BODY,{"derivedFrom":makeQuery(id+"F2.opPattern","COPY",BODY,{"derivedFrom":makeQuery(id+"F1.opRevolve","SWEPT_BODY",BODY,{"disambiguationData":[OSD([sQuery(id+"F0.wireOp",EDGE,"E1")])]}),"instanceName":"1"}),"instanceName":"1"}),"instanceName":"1"}),"instanceName":"1"}),"instanceName":"1"}),"instanceName":"1"}),"instanceName":"1"}),"instanceName":"1"});
            var Q1470;
            Q1470=makeQuery(id+"F12.opPattern","COPY",BODY,{"derivedFrom":makeQuery(id+"F11.opPattern","COPY",BODY,{"derivedFrom":makeQuery(id+"F10.opPattern","COPY",BODY,{"derivedFrom":makeQuery(id+"F9.opPattern","COPY",BODY,{"derivedFrom":makeQuery(id+"F7.opPattern","COPY",BODY,{"derivedFrom":makeQuery(id+"F5.opPattern","COPY",BODY,{"derivedFrom":makeQuery(id+"F1.opRevolve","SWEPT_BODY",BODY,{"disambiguationData":[OSD([sQuery(id+"F0.wireOp",EDGE,"E1")])]}),"instanceName":"1"}),"instanceName":"1"}),"instanceName":"1"}),"instanceName":"1"}),"instanceName":"1"}),"instanceName":"1"});
            var Q1471;
            Q1471=makeQuery(id+"F12.opPattern","COPY",BODY,{"derivedFrom":makeQuery(id+"F11.opPattern","COPY",BODY,{"derivedFrom":makeQuery(id+"F10.opPattern","COPY",BODY,{"derivedFrom":makeQuery(id+"F9.opPattern","COPY",BODY,{"derivedFrom":makeQuery(id+"F7.opPattern","COPY",BODY,{"derivedFrom":makeQuery(id+"F5.opPattern","COPY",BODY,{"derivedFrom":makeQuery(id+"F2.opPattern","COPY",BODY,{"derivedFrom":makeQuery(id+"F1.opRevolve","SWEPT_BODY",BODY,{"disambiguationData":[OSD([sQuery(id+"F0.wireOp",EDGE,"E1")])]}),"instanceName":"1"}),"instanceName":"1"}),"instanceName":"1"}),"instanceName":"1"}),"instanceName":"1"}),"instanceName":"1"}),"instanceName":"1"});
            var Q1472;
            Q1472=makeQuery(id+"F12.opPattern","COPY",BODY,{"derivedFrom":makeQuery(id+"F11.opPattern","COPY",BODY,{"derivedFrom":makeQuery(id+"F10.opPattern","COPY",BODY,{"derivedFrom":makeQuery(id+"F9.opPattern","COPY",BODY,{"derivedFrom":makeQuery(id+"F7.opPattern","COPY",BODY,{"derivedFrom":makeQuery(id+"F5.opPattern","COPY",BODY,{"derivedFrom":makeQuery(id+"F3.opPattern","COPY",BODY,{"derivedFrom":makeQuery(id+"F2.opPattern","COPY",BODY,{"derivedFrom":makeQuery(id+"F1.opRevolve","SWEPT_BODY",BODY,{"disambiguationData":[OSD([sQuery(id+"F0.wireOp",EDGE,"E1")])]}),"instanceName":"1"}),"instanceName":"1"}),"instanceName":"1"}),"instanceName":"1"}),"instanceName":"1"}),"instanceName":"1"}),"instanceName":"1"}),"instanceName":"1"});
            var Q1473;
            Q1473=makeQuery(id+"F12.opPattern","COPY",BODY,{"derivedFrom":makeQuery(id+"F11.opPattern","COPY",BODY,{"derivedFrom":makeQuery(id+"F10.opPattern","COPY",BODY,{"derivedFrom":makeQuery(id+"F9.opPattern","COPY",BODY,{"derivedFrom":makeQuery(id+"F7.opPattern","COPY",BODY,{"derivedFrom":makeQuery(id+"F5.opPattern","COPY",BODY,{"derivedFrom":makeQuery(id+"F4.opPattern","COPY",BODY,{"derivedFrom":makeQuery(id+"F1.opRevolve","SWEPT_BODY",BODY,{"disambiguationData":[OSD([sQuery(id+"F0.wireOp",EDGE,"E1")])]}),"instanceName":"1"}),"instanceName":"1"}),"instanceName":"1"}),"instanceName":"1"}),"instanceName":"1"}),"instanceName":"1"}),"instanceName":"1"});
            var Q1474;
            Q1474=makeQuery(id+"F12.opPattern","COPY",BODY,{"derivedFrom":makeQuery(id+"F11.opPattern","COPY",BODY,{"derivedFrom":makeQuery(id+"F10.opPattern","COPY",BODY,{"derivedFrom":makeQuery(id+"F9.opPattern","COPY",BODY,{"derivedFrom":makeQuery(id+"F7.opPattern","COPY",BODY,{"derivedFrom":makeQuery(id+"F5.opPattern","COPY",BODY,{"derivedFrom":makeQuery(id+"F4.opPattern","COPY",BODY,{"derivedFrom":makeQuery(id+"F2.opPattern","COPY",BODY,{"derivedFrom":makeQuery(id+"F1.opRevolve","SWEPT_BODY",BODY,{"disambiguationData":[OSD([sQuery(id+"F0.wireOp",EDGE,"E1")])]}),"instanceName":"1"}),"instanceName":"1"}),"instanceName":"1"}),"instanceName":"1"}),"instanceName":"1"}),"instanceName":"1"}),"instanceName":"1"}),"instanceName":"1"});
            var Q1475;
            Q1475=makeQuery(id+"F12.opPattern","COPY",BODY,{"derivedFrom":makeQuery(id+"F11.opPattern","COPY",BODY,{"derivedFrom":makeQuery(id+"F10.opPattern","COPY",BODY,{"derivedFrom":makeQuery(id+"F9.opPattern","COPY",BODY,{"derivedFrom":makeQuery(id+"F7.opPattern","COPY",BODY,{"derivedFrom":makeQuery(id+"F5.opPattern","COPY",BODY,{"derivedFrom":makeQuery(id+"F4.opPattern","COPY",BODY,{"derivedFrom":makeQuery(id+"F3.opPattern","COPY",BODY,{"derivedFrom":makeQuery(id+"F2.opPattern","COPY",BODY,{"derivedFrom":makeQuery(id+"F1.opRevolve","SWEPT_BODY",BODY,{"disambiguationData":[OSD([sQuery(id+"F0.wireOp",EDGE,"E1")])]}),"instanceName":"1"}),"instanceName":"1"}),"instanceName":"1"}),"instanceName":"1"}),"instanceName":"1"}),"instanceName":"1"}),"instanceName":"1"}),"instanceName":"1"}),"instanceName":"1"});
            var Q1476;
            Q1476=makeQuery(id+"F12.opPattern","COPY",BODY,{"derivedFrom":makeQuery(id+"F11.opPattern","COPY",BODY,{"derivedFrom":makeQuery(id+"F10.opPattern","COPY",BODY,{"derivedFrom":makeQuery(id+"F9.opPattern","COPY",BODY,{"derivedFrom":makeQuery(id+"F7.opPattern","COPY",BODY,{"derivedFrom":makeQuery(id+"F6.opPattern","COPY",BODY,{"derivedFrom":makeQuery(id+"F1.opRevolve","SWEPT_BODY",BODY,{"disambiguationData":[OSD([sQuery(id+"F0.wireOp",EDGE,"E1")])]}),"instanceName":"1"}),"instanceName":"1"}),"instanceName":"1"}),"instanceName":"1"}),"instanceName":"1"}),"instanceName":"1"});
            var Q1477;
            Q1477=makeQuery(id+"F12.opPattern","COPY",BODY,{"derivedFrom":makeQuery(id+"F11.opPattern","COPY",BODY,{"derivedFrom":makeQuery(id+"F10.opPattern","COPY",BODY,{"derivedFrom":makeQuery(id+"F9.opPattern","COPY",BODY,{"derivedFrom":makeQuery(id+"F7.opPattern","COPY",BODY,{"derivedFrom":makeQuery(id+"F6.opPattern","COPY",BODY,{"derivedFrom":makeQuery(id+"F2.opPattern","COPY",BODY,{"derivedFrom":makeQuery(id+"F1.opRevolve","SWEPT_BODY",BODY,{"disambiguationData":[OSD([sQuery(id+"F0.wireOp",EDGE,"E1")])]}),"instanceName":"1"}),"instanceName":"1"}),"instanceName":"1"}),"instanceName":"1"}),"instanceName":"1"}),"instanceName":"1"}),"instanceName":"1"});
            var Q1478;
            Q1478=makeQuery(id+"F12.opPattern","COPY",BODY,{"derivedFrom":makeQuery(id+"F11.opPattern","COPY",BODY,{"derivedFrom":makeQuery(id+"F10.opPattern","COPY",BODY,{"derivedFrom":makeQuery(id+"F9.opPattern","COPY",BODY,{"derivedFrom":makeQuery(id+"F7.opPattern","COPY",BODY,{"derivedFrom":makeQuery(id+"F6.opPattern","COPY",BODY,{"derivedFrom":makeQuery(id+"F3.opPattern","COPY",BODY,{"derivedFrom":makeQuery(id+"F2.opPattern","COPY",BODY,{"derivedFrom":makeQuery(id+"F1.opRevolve","SWEPT_BODY",BODY,{"disambiguationData":[OSD([sQuery(id+"F0.wireOp",EDGE,"E1")])]}),"instanceName":"1"}),"instanceName":"1"}),"instanceName":"1"}),"instanceName":"1"}),"instanceName":"1"}),"instanceName":"1"}),"instanceName":"1"}),"instanceName":"1"});
            var Q1479;
            Q1479=makeQuery(id+"F12.opPattern","COPY",BODY,{"derivedFrom":makeQuery(id+"F11.opPattern","COPY",BODY,{"derivedFrom":makeQuery(id+"F10.opPattern","COPY",BODY,{"derivedFrom":makeQuery(id+"F9.opPattern","COPY",BODY,{"derivedFrom":makeQuery(id+"F7.opPattern","COPY",BODY,{"derivedFrom":makeQuery(id+"F6.opPattern","COPY",BODY,{"derivedFrom":makeQuery(id+"F4.opPattern","COPY",BODY,{"derivedFrom":makeQuery(id+"F1.opRevolve","SWEPT_BODY",BODY,{"disambiguationData":[OSD([sQuery(id+"F0.wireOp",EDGE,"E1")])]}),"instanceName":"1"}),"instanceName":"1"}),"instanceName":"1"}),"instanceName":"1"}),"instanceName":"1"}),"instanceName":"1"}),"instanceName":"1"});
            var Q1480;
            Q1480=makeQuery(id+"F12.opPattern","COPY",BODY,{"derivedFrom":makeQuery(id+"F11.opPattern","COPY",BODY,{"derivedFrom":makeQuery(id+"F10.opPattern","COPY",BODY,{"derivedFrom":makeQuery(id+"F9.opPattern","COPY",BODY,{"derivedFrom":makeQuery(id+"F7.opPattern","COPY",BODY,{"derivedFrom":makeQuery(id+"F6.opPattern","COPY",BODY,{"derivedFrom":makeQuery(id+"F4.opPattern","COPY",BODY,{"derivedFrom":makeQuery(id+"F2.opPattern","COPY",BODY,{"derivedFrom":makeQuery(id+"F1.opRevolve","SWEPT_BODY",BODY,{"disambiguationData":[OSD([sQuery(id+"F0.wireOp",EDGE,"E1")])]}),"instanceName":"1"}),"instanceName":"1"}),"instanceName":"1"}),"instanceName":"1"}),"instanceName":"1"}),"instanceName":"1"}),"instanceName":"1"}),"instanceName":"1"});
            var Q1481;
            Q1481=makeQuery(id+"F12.opPattern","COPY",BODY,{"derivedFrom":makeQuery(id+"F11.opPattern","COPY",BODY,{"derivedFrom":makeQuery(id+"F10.opPattern","COPY",BODY,{"derivedFrom":makeQuery(id+"F9.opPattern","COPY",BODY,{"derivedFrom":makeQuery(id+"F7.opPattern","COPY",BODY,{"derivedFrom":makeQuery(id+"F6.opPattern","COPY",BODY,{"derivedFrom":makeQuery(id+"F4.opPattern","COPY",BODY,{"derivedFrom":makeQuery(id+"F3.opPattern","COPY",BODY,{"derivedFrom":makeQuery(id+"F2.opPattern","COPY",BODY,{"derivedFrom":makeQuery(id+"F1.opRevolve","SWEPT_BODY",BODY,{"disambiguationData":[OSD([sQuery(id+"F0.wireOp",EDGE,"E1")])]}),"instanceName":"1"}),"instanceName":"1"}),"instanceName":"1"}),"instanceName":"1"}),"instanceName":"1"}),"instanceName":"1"}),"instanceName":"1"}),"instanceName":"1"}),"instanceName":"1"});
            var Q1482;
            Q1482=makeQuery(id+"F12.opPattern","COPY",BODY,{"derivedFrom":makeQuery(id+"F11.opPattern","COPY",BODY,{"derivedFrom":makeQuery(id+"F10.opPattern","COPY",BODY,{"derivedFrom":makeQuery(id+"F9.opPattern","COPY",BODY,{"derivedFrom":makeQuery(id+"F7.opPattern","COPY",BODY,{"derivedFrom":makeQuery(id+"F6.opPattern","COPY",BODY,{"derivedFrom":makeQuery(id+"F5.opPattern","COPY",BODY,{"derivedFrom":makeQuery(id+"F1.opRevolve","SWEPT_BODY",BODY,{"disambiguationData":[OSD([sQuery(id+"F0.wireOp",EDGE,"E1")])]}),"instanceName":"1"}),"instanceName":"1"}),"instanceName":"1"}),"instanceName":"1"}),"instanceName":"1"}),"instanceName":"1"}),"instanceName":"1"});
            var Q1483;
            Q1483=makeQuery(id+"F12.opPattern","COPY",BODY,{"derivedFrom":makeQuery(id+"F11.opPattern","COPY",BODY,{"derivedFrom":makeQuery(id+"F10.opPattern","COPY",BODY,{"derivedFrom":makeQuery(id+"F9.opPattern","COPY",BODY,{"derivedFrom":makeQuery(id+"F7.opPattern","COPY",BODY,{"derivedFrom":makeQuery(id+"F6.opPattern","COPY",BODY,{"derivedFrom":makeQuery(id+"F5.opPattern","COPY",BODY,{"derivedFrom":makeQuery(id+"F2.opPattern","COPY",BODY,{"derivedFrom":makeQuery(id+"F1.opRevolve","SWEPT_BODY",BODY,{"disambiguationData":[OSD([sQuery(id+"F0.wireOp",EDGE,"E1")])]}),"instanceName":"1"}),"instanceName":"1"}),"instanceName":"1"}),"instanceName":"1"}),"instanceName":"1"}),"instanceName":"1"}),"instanceName":"1"}),"instanceName":"1"});
            var Q1484;
            Q1484=makeQuery(id+"F12.opPattern","COPY",BODY,{"derivedFrom":makeQuery(id+"F11.opPattern","COPY",BODY,{"derivedFrom":makeQuery(id+"F10.opPattern","COPY",BODY,{"derivedFrom":makeQuery(id+"F9.opPattern","COPY",BODY,{"derivedFrom":makeQuery(id+"F7.opPattern","COPY",BODY,{"derivedFrom":makeQuery(id+"F6.opPattern","COPY",BODY,{"derivedFrom":makeQuery(id+"F5.opPattern","COPY",BODY,{"derivedFrom":makeQuery(id+"F3.opPattern","COPY",BODY,{"derivedFrom":makeQuery(id+"F2.opPattern","COPY",BODY,{"derivedFrom":makeQuery(id+"F1.opRevolve","SWEPT_BODY",BODY,{"disambiguationData":[OSD([sQuery(id+"F0.wireOp",EDGE,"E1")])]}),"instanceName":"1"}),"instanceName":"1"}),"instanceName":"1"}),"instanceName":"1"}),"instanceName":"1"}),"instanceName":"1"}),"instanceName":"1"}),"instanceName":"1"}),"instanceName":"1"});
            var Q1485;
            Q1485=makeQuery(id+"F12.opPattern","COPY",BODY,{"derivedFrom":makeQuery(id+"F11.opPattern","COPY",BODY,{"derivedFrom":makeQuery(id+"F10.opPattern","COPY",BODY,{"derivedFrom":makeQuery(id+"F9.opPattern","COPY",BODY,{"derivedFrom":makeQuery(id+"F7.opPattern","COPY",BODY,{"derivedFrom":makeQuery(id+"F6.opPattern","COPY",BODY,{"derivedFrom":makeQuery(id+"F5.opPattern","COPY",BODY,{"derivedFrom":makeQuery(id+"F4.opPattern","COPY",BODY,{"derivedFrom":makeQuery(id+"F1.opRevolve","SWEPT_BODY",BODY,{"disambiguationData":[OSD([sQuery(id+"F0.wireOp",EDGE,"E1")])]}),"instanceName":"1"}),"instanceName":"1"}),"instanceName":"1"}),"instanceName":"1"}),"instanceName":"1"}),"instanceName":"1"}),"instanceName":"1"}),"instanceName":"1"});
            var Q1486;
            Q1486=makeQuery(id+"F12.opPattern","COPY",BODY,{"derivedFrom":makeQuery(id+"F11.opPattern","COPY",BODY,{"derivedFrom":makeQuery(id+"F10.opPattern","COPY",BODY,{"derivedFrom":makeQuery(id+"F9.opPattern","COPY",BODY,{"derivedFrom":makeQuery(id+"F7.opPattern","COPY",BODY,{"derivedFrom":makeQuery(id+"F6.opPattern","COPY",BODY,{"derivedFrom":makeQuery(id+"F5.opPattern","COPY",BODY,{"derivedFrom":makeQuery(id+"F4.opPattern","COPY",BODY,{"derivedFrom":makeQuery(id+"F2.opPattern","COPY",BODY,{"derivedFrom":makeQuery(id+"F1.opRevolve","SWEPT_BODY",BODY,{"disambiguationData":[OSD([sQuery(id+"F0.wireOp",EDGE,"E1")])]}),"instanceName":"1"}),"instanceName":"1"}),"instanceName":"1"}),"instanceName":"1"}),"instanceName":"1"}),"instanceName":"1"}),"instanceName":"1"}),"instanceName":"1"}),"instanceName":"1"});
            var Q1487;
            Q1487=makeQuery(id+"F12.opPattern","COPY",BODY,{"derivedFrom":makeQuery(id+"F11.opPattern","COPY",BODY,{"derivedFrom":makeQuery(id+"F10.opPattern","COPY",BODY,{"derivedFrom":makeQuery(id+"F9.opPattern","COPY",BODY,{"derivedFrom":makeQuery(id+"F7.opPattern","COPY",BODY,{"derivedFrom":makeQuery(id+"F6.opPattern","COPY",BODY,{"derivedFrom":makeQuery(id+"F5.opPattern","COPY",BODY,{"derivedFrom":makeQuery(id+"F4.opPattern","COPY",BODY,{"derivedFrom":makeQuery(id+"F3.opPattern","COPY",BODY,{"derivedFrom":makeQuery(id+"F2.opPattern","COPY",BODY,{"derivedFrom":makeQuery(id+"F1.opRevolve","SWEPT_BODY",BODY,{"disambiguationData":[OSD([sQuery(id+"F0.wireOp",EDGE,"E1")])]}),"instanceName":"1"}),"instanceName":"1"}),"instanceName":"1"}),"instanceName":"1"}),"instanceName":"1"}),"instanceName":"1"}),"instanceName":"1"}),"instanceName":"1"}),"instanceName":"1"}),"instanceName":"1"});
            var Q1488;
            Q1488=makeQuery(id+"F12.opPattern","COPY",BODY,{"derivedFrom":makeQuery(id+"F11.opPattern","COPY",BODY,{"derivedFrom":makeQuery(id+"F10.opPattern","COPY",BODY,{"derivedFrom":makeQuery(id+"F9.opPattern","COPY",BODY,{"derivedFrom":makeQuery(id+"F8.opPattern","COPY",BODY,{"derivedFrom":makeQuery(id+"F1.opRevolve","SWEPT_BODY",BODY,{"disambiguationData":[OSD([sQuery(id+"F0.wireOp",EDGE,"E1")])]}),"instanceName":"1"}),"instanceName":"1"}),"instanceName":"1"}),"instanceName":"1"}),"instanceName":"1"});
            var Q1489;
            Q1489=makeQuery(id+"F12.opPattern","COPY",BODY,{"derivedFrom":makeQuery(id+"F11.opPattern","COPY",BODY,{"derivedFrom":makeQuery(id+"F10.opPattern","COPY",BODY,{"derivedFrom":makeQuery(id+"F9.opPattern","COPY",BODY,{"derivedFrom":makeQuery(id+"F8.opPattern","COPY",BODY,{"derivedFrom":makeQuery(id+"F2.opPattern","COPY",BODY,{"derivedFrom":makeQuery(id+"F1.opRevolve","SWEPT_BODY",BODY,{"disambiguationData":[OSD([sQuery(id+"F0.wireOp",EDGE,"E1")])]}),"instanceName":"1"}),"instanceName":"1"}),"instanceName":"1"}),"instanceName":"1"}),"instanceName":"1"}),"instanceName":"1"});
            var Q1490;
            Q1490=makeQuery(id+"F12.opPattern","COPY",BODY,{"derivedFrom":makeQuery(id+"F11.opPattern","COPY",BODY,{"derivedFrom":makeQuery(id+"F10.opPattern","COPY",BODY,{"derivedFrom":makeQuery(id+"F9.opPattern","COPY",BODY,{"derivedFrom":makeQuery(id+"F8.opPattern","COPY",BODY,{"derivedFrom":makeQuery(id+"F3.opPattern","COPY",BODY,{"derivedFrom":makeQuery(id+"F2.opPattern","COPY",BODY,{"derivedFrom":makeQuery(id+"F1.opRevolve","SWEPT_BODY",BODY,{"disambiguationData":[OSD([sQuery(id+"F0.wireOp",EDGE,"E1")])]}),"instanceName":"1"}),"instanceName":"1"}),"instanceName":"1"}),"instanceName":"1"}),"instanceName":"1"}),"instanceName":"1"}),"instanceName":"1"});
            var Q1491;
            Q1491=makeQuery(id+"F12.opPattern","COPY",BODY,{"derivedFrom":makeQuery(id+"F11.opPattern","COPY",BODY,{"derivedFrom":makeQuery(id+"F10.opPattern","COPY",BODY,{"derivedFrom":makeQuery(id+"F9.opPattern","COPY",BODY,{"derivedFrom":makeQuery(id+"F8.opPattern","COPY",BODY,{"derivedFrom":makeQuery(id+"F4.opPattern","COPY",BODY,{"derivedFrom":makeQuery(id+"F1.opRevolve","SWEPT_BODY",BODY,{"disambiguationData":[OSD([sQuery(id+"F0.wireOp",EDGE,"E1")])]}),"instanceName":"1"}),"instanceName":"1"}),"instanceName":"1"}),"instanceName":"1"}),"instanceName":"1"}),"instanceName":"1"});
            var Q1492;
            Q1492=makeQuery(id+"F12.opPattern","COPY",BODY,{"derivedFrom":makeQuery(id+"F11.opPattern","COPY",BODY,{"derivedFrom":makeQuery(id+"F10.opPattern","COPY",BODY,{"derivedFrom":makeQuery(id+"F9.opPattern","COPY",BODY,{"derivedFrom":makeQuery(id+"F8.opPattern","COPY",BODY,{"derivedFrom":makeQuery(id+"F4.opPattern","COPY",BODY,{"derivedFrom":makeQuery(id+"F2.opPattern","COPY",BODY,{"derivedFrom":makeQuery(id+"F1.opRevolve","SWEPT_BODY",BODY,{"disambiguationData":[OSD([sQuery(id+"F0.wireOp",EDGE,"E1")])]}),"instanceName":"1"}),"instanceName":"1"}),"instanceName":"1"}),"instanceName":"1"}),"instanceName":"1"}),"instanceName":"1"}),"instanceName":"1"});
            var Q1493;
            Q1493=makeQuery(id+"F12.opPattern","COPY",BODY,{"derivedFrom":makeQuery(id+"F11.opPattern","COPY",BODY,{"derivedFrom":makeQuery(id+"F10.opPattern","COPY",BODY,{"derivedFrom":makeQuery(id+"F9.opPattern","COPY",BODY,{"derivedFrom":makeQuery(id+"F8.opPattern","COPY",BODY,{"derivedFrom":makeQuery(id+"F4.opPattern","COPY",BODY,{"derivedFrom":makeQuery(id+"F3.opPattern","COPY",BODY,{"derivedFrom":makeQuery(id+"F2.opPattern","COPY",BODY,{"derivedFrom":makeQuery(id+"F1.opRevolve","SWEPT_BODY",BODY,{"disambiguationData":[OSD([sQuery(id+"F0.wireOp",EDGE,"E1")])]}),"instanceName":"1"}),"instanceName":"1"}),"instanceName":"1"}),"instanceName":"1"}),"instanceName":"1"}),"instanceName":"1"}),"instanceName":"1"}),"instanceName":"1"});
            var Q1494;
            Q1494=makeQuery(id+"F12.opPattern","COPY",BODY,{"derivedFrom":makeQuery(id+"F11.opPattern","COPY",BODY,{"derivedFrom":makeQuery(id+"F10.opPattern","COPY",BODY,{"derivedFrom":makeQuery(id+"F9.opPattern","COPY",BODY,{"derivedFrom":makeQuery(id+"F8.opPattern","COPY",BODY,{"derivedFrom":makeQuery(id+"F5.opPattern","COPY",BODY,{"derivedFrom":makeQuery(id+"F1.opRevolve","SWEPT_BODY",BODY,{"disambiguationData":[OSD([sQuery(id+"F0.wireOp",EDGE,"E1")])]}),"instanceName":"1"}),"instanceName":"1"}),"instanceName":"1"}),"instanceName":"1"}),"instanceName":"1"}),"instanceName":"1"});
            var Q1495;
            Q1495=makeQuery(id+"F12.opPattern","COPY",BODY,{"derivedFrom":makeQuery(id+"F11.opPattern","COPY",BODY,{"derivedFrom":makeQuery(id+"F10.opPattern","COPY",BODY,{"derivedFrom":makeQuery(id+"F9.opPattern","COPY",BODY,{"derivedFrom":makeQuery(id+"F8.opPattern","COPY",BODY,{"derivedFrom":makeQuery(id+"F5.opPattern","COPY",BODY,{"derivedFrom":makeQuery(id+"F2.opPattern","COPY",BODY,{"derivedFrom":makeQuery(id+"F1.opRevolve","SWEPT_BODY",BODY,{"disambiguationData":[OSD([sQuery(id+"F0.wireOp",EDGE,"E1")])]}),"instanceName":"1"}),"instanceName":"1"}),"instanceName":"1"}),"instanceName":"1"}),"instanceName":"1"}),"instanceName":"1"}),"instanceName":"1"});
            var Q1496;
            Q1496=makeQuery(id+"F12.opPattern","COPY",BODY,{"derivedFrom":makeQuery(id+"F11.opPattern","COPY",BODY,{"derivedFrom":makeQuery(id+"F10.opPattern","COPY",BODY,{"derivedFrom":makeQuery(id+"F9.opPattern","COPY",BODY,{"derivedFrom":makeQuery(id+"F8.opPattern","COPY",BODY,{"derivedFrom":makeQuery(id+"F5.opPattern","COPY",BODY,{"derivedFrom":makeQuery(id+"F3.opPattern","COPY",BODY,{"derivedFrom":makeQuery(id+"F2.opPattern","COPY",BODY,{"derivedFrom":makeQuery(id+"F1.opRevolve","SWEPT_BODY",BODY,{"disambiguationData":[OSD([sQuery(id+"F0.wireOp",EDGE,"E1")])]}),"instanceName":"1"}),"instanceName":"1"}),"instanceName":"1"}),"instanceName":"1"}),"instanceName":"1"}),"instanceName":"1"}),"instanceName":"1"}),"instanceName":"1"});
            var Q1497;
            Q1497=makeQuery(id+"F12.opPattern","COPY",BODY,{"derivedFrom":makeQuery(id+"F11.opPattern","COPY",BODY,{"derivedFrom":makeQuery(id+"F10.opPattern","COPY",BODY,{"derivedFrom":makeQuery(id+"F9.opPattern","COPY",BODY,{"derivedFrom":makeQuery(id+"F8.opPattern","COPY",BODY,{"derivedFrom":makeQuery(id+"F5.opPattern","COPY",BODY,{"derivedFrom":makeQuery(id+"F4.opPattern","COPY",BODY,{"derivedFrom":makeQuery(id+"F1.opRevolve","SWEPT_BODY",BODY,{"disambiguationData":[OSD([sQuery(id+"F0.wireOp",EDGE,"E1")])]}),"instanceName":"1"}),"instanceName":"1"}),"instanceName":"1"}),"instanceName":"1"}),"instanceName":"1"}),"instanceName":"1"}),"instanceName":"1"});
            var Q1498;
            Q1498=makeQuery(id+"F12.opPattern","COPY",BODY,{"derivedFrom":makeQuery(id+"F11.opPattern","COPY",BODY,{"derivedFrom":makeQuery(id+"F10.opPattern","COPY",BODY,{"derivedFrom":makeQuery(id+"F9.opPattern","COPY",BODY,{"derivedFrom":makeQuery(id+"F8.opPattern","COPY",BODY,{"derivedFrom":makeQuery(id+"F5.opPattern","COPY",BODY,{"derivedFrom":makeQuery(id+"F4.opPattern","COPY",BODY,{"derivedFrom":makeQuery(id+"F2.opPattern","COPY",BODY,{"derivedFrom":makeQuery(id+"F1.opRevolve","SWEPT_BODY",BODY,{"disambiguationData":[OSD([sQuery(id+"F0.wireOp",EDGE,"E1")])]}),"instanceName":"1"}),"instanceName":"1"}),"instanceName":"1"}),"instanceName":"1"}),"instanceName":"1"}),"instanceName":"1"}),"instanceName":"1"}),"instanceName":"1"});
            var Q1499;
            Q1499=makeQuery(id+"F12.opPattern","COPY",BODY,{"derivedFrom":makeQuery(id+"F11.opPattern","COPY",BODY,{"derivedFrom":makeQuery(id+"F10.opPattern","COPY",BODY,{"derivedFrom":makeQuery(id+"F9.opPattern","COPY",BODY,{"derivedFrom":makeQuery(id+"F8.opPattern","COPY",BODY,{"derivedFrom":makeQuery(id+"F5.opPattern","COPY",BODY,{"derivedFrom":makeQuery(id+"F4.opPattern","COPY",BODY,{"derivedFrom":makeQuery(id+"F3.opPattern","COPY",BODY,{"derivedFrom":makeQuery(id+"F2.opPattern","COPY",BODY,{"derivedFrom":makeQuery(id+"F1.opRevolve","SWEPT_BODY",BODY,{"disambiguationData":[OSD([sQuery(id+"F0.wireOp",EDGE,"E1")])]}),"instanceName":"1"}),"instanceName":"1"}),"instanceName":"1"}),"instanceName":"1"}),"instanceName":"1"}),"instanceName":"1"}),"instanceName":"1"}),"instanceName":"1"}),"instanceName":"1"});
            var Q1500;
            Q1500=makeQuery(id+"F12.opPattern","COPY",BODY,{"derivedFrom":makeQuery(id+"F11.opPattern","COPY",BODY,{"derivedFrom":makeQuery(id+"F10.opPattern","COPY",BODY,{"derivedFrom":makeQuery(id+"F9.opPattern","COPY",BODY,{"derivedFrom":makeQuery(id+"F8.opPattern","COPY",BODY,{"derivedFrom":makeQuery(id+"F6.opPattern","COPY",BODY,{"derivedFrom":makeQuery(id+"F1.opRevolve","SWEPT_BODY",BODY,{"disambiguationData":[OSD([sQuery(id+"F0.wireOp",EDGE,"E1")])]}),"instanceName":"1"}),"instanceName":"1"}),"instanceName":"1"}),"instanceName":"1"}),"instanceName":"1"}),"instanceName":"1"});
            var Q1501;
            Q1501=makeQuery(id+"F12.opPattern","COPY",BODY,{"derivedFrom":makeQuery(id+"F11.opPattern","COPY",BODY,{"derivedFrom":makeQuery(id+"F10.opPattern","COPY",BODY,{"derivedFrom":makeQuery(id+"F9.opPattern","COPY",BODY,{"derivedFrom":makeQuery(id+"F8.opPattern","COPY",BODY,{"derivedFrom":makeQuery(id+"F6.opPattern","COPY",BODY,{"derivedFrom":makeQuery(id+"F2.opPattern","COPY",BODY,{"derivedFrom":makeQuery(id+"F1.opRevolve","SWEPT_BODY",BODY,{"disambiguationData":[OSD([sQuery(id+"F0.wireOp",EDGE,"E1")])]}),"instanceName":"1"}),"instanceName":"1"}),"instanceName":"1"}),"instanceName":"1"}),"instanceName":"1"}),"instanceName":"1"}),"instanceName":"1"});
            var Q1502;
            Q1502=makeQuery(id+"F12.opPattern","COPY",BODY,{"derivedFrom":makeQuery(id+"F11.opPattern","COPY",BODY,{"derivedFrom":makeQuery(id+"F10.opPattern","COPY",BODY,{"derivedFrom":makeQuery(id+"F9.opPattern","COPY",BODY,{"derivedFrom":makeQuery(id+"F8.opPattern","COPY",BODY,{"derivedFrom":makeQuery(id+"F6.opPattern","COPY",BODY,{"derivedFrom":makeQuery(id+"F3.opPattern","COPY",BODY,{"derivedFrom":makeQuery(id+"F2.opPattern","COPY",BODY,{"derivedFrom":makeQuery(id+"F1.opRevolve","SWEPT_BODY",BODY,{"disambiguationData":[OSD([sQuery(id+"F0.wireOp",EDGE,"E1")])]}),"instanceName":"1"}),"instanceName":"1"}),"instanceName":"1"}),"instanceName":"1"}),"instanceName":"1"}),"instanceName":"1"}),"instanceName":"1"}),"instanceName":"1"});
            var Q1503;
            Q1503=makeQuery(id+"F12.opPattern","COPY",BODY,{"derivedFrom":makeQuery(id+"F11.opPattern","COPY",BODY,{"derivedFrom":makeQuery(id+"F10.opPattern","COPY",BODY,{"derivedFrom":makeQuery(id+"F9.opPattern","COPY",BODY,{"derivedFrom":makeQuery(id+"F8.opPattern","COPY",BODY,{"derivedFrom":makeQuery(id+"F6.opPattern","COPY",BODY,{"derivedFrom":makeQuery(id+"F4.opPattern","COPY",BODY,{"derivedFrom":makeQuery(id+"F1.opRevolve","SWEPT_BODY",BODY,{"disambiguationData":[OSD([sQuery(id+"F0.wireOp",EDGE,"E1")])]}),"instanceName":"1"}),"instanceName":"1"}),"instanceName":"1"}),"instanceName":"1"}),"instanceName":"1"}),"instanceName":"1"}),"instanceName":"1"});
            var Q1504;
            Q1504=makeQuery(id+"F12.opPattern","COPY",BODY,{"derivedFrom":makeQuery(id+"F11.opPattern","COPY",BODY,{"derivedFrom":makeQuery(id+"F10.opPattern","COPY",BODY,{"derivedFrom":makeQuery(id+"F9.opPattern","COPY",BODY,{"derivedFrom":makeQuery(id+"F8.opPattern","COPY",BODY,{"derivedFrom":makeQuery(id+"F6.opPattern","COPY",BODY,{"derivedFrom":makeQuery(id+"F4.opPattern","COPY",BODY,{"derivedFrom":makeQuery(id+"F2.opPattern","COPY",BODY,{"derivedFrom":makeQuery(id+"F1.opRevolve","SWEPT_BODY",BODY,{"disambiguationData":[OSD([sQuery(id+"F0.wireOp",EDGE,"E1")])]}),"instanceName":"1"}),"instanceName":"1"}),"instanceName":"1"}),"instanceName":"1"}),"instanceName":"1"}),"instanceName":"1"}),"instanceName":"1"}),"instanceName":"1"});
            var Q1505;
            Q1505=makeQuery(id+"F12.opPattern","COPY",BODY,{"derivedFrom":makeQuery(id+"F11.opPattern","COPY",BODY,{"derivedFrom":makeQuery(id+"F10.opPattern","COPY",BODY,{"derivedFrom":makeQuery(id+"F9.opPattern","COPY",BODY,{"derivedFrom":makeQuery(id+"F8.opPattern","COPY",BODY,{"derivedFrom":makeQuery(id+"F6.opPattern","COPY",BODY,{"derivedFrom":makeQuery(id+"F4.opPattern","COPY",BODY,{"derivedFrom":makeQuery(id+"F3.opPattern","COPY",BODY,{"derivedFrom":makeQuery(id+"F2.opPattern","COPY",BODY,{"derivedFrom":makeQuery(id+"F1.opRevolve","SWEPT_BODY",BODY,{"disambiguationData":[OSD([sQuery(id+"F0.wireOp",EDGE,"E1")])]}),"instanceName":"1"}),"instanceName":"1"}),"instanceName":"1"}),"instanceName":"1"}),"instanceName":"1"}),"instanceName":"1"}),"instanceName":"1"}),"instanceName":"1"}),"instanceName":"1"});
            var Q1506;
            Q1506=makeQuery(id+"F12.opPattern","COPY",BODY,{"derivedFrom":makeQuery(id+"F11.opPattern","COPY",BODY,{"derivedFrom":makeQuery(id+"F10.opPattern","COPY",BODY,{"derivedFrom":makeQuery(id+"F9.opPattern","COPY",BODY,{"derivedFrom":makeQuery(id+"F8.opPattern","COPY",BODY,{"derivedFrom":makeQuery(id+"F6.opPattern","COPY",BODY,{"derivedFrom":makeQuery(id+"F5.opPattern","COPY",BODY,{"derivedFrom":makeQuery(id+"F1.opRevolve","SWEPT_BODY",BODY,{"disambiguationData":[OSD([sQuery(id+"F0.wireOp",EDGE,"E1")])]}),"instanceName":"1"}),"instanceName":"1"}),"instanceName":"1"}),"instanceName":"1"}),"instanceName":"1"}),"instanceName":"1"}),"instanceName":"1"});
            var Q1507;
            Q1507=makeQuery(id+"F12.opPattern","COPY",BODY,{"derivedFrom":makeQuery(id+"F11.opPattern","COPY",BODY,{"derivedFrom":makeQuery(id+"F10.opPattern","COPY",BODY,{"derivedFrom":makeQuery(id+"F9.opPattern","COPY",BODY,{"derivedFrom":makeQuery(id+"F8.opPattern","COPY",BODY,{"derivedFrom":makeQuery(id+"F6.opPattern","COPY",BODY,{"derivedFrom":makeQuery(id+"F5.opPattern","COPY",BODY,{"derivedFrom":makeQuery(id+"F2.opPattern","COPY",BODY,{"derivedFrom":makeQuery(id+"F1.opRevolve","SWEPT_BODY",BODY,{"disambiguationData":[OSD([sQuery(id+"F0.wireOp",EDGE,"E1")])]}),"instanceName":"1"}),"instanceName":"1"}),"instanceName":"1"}),"instanceName":"1"}),"instanceName":"1"}),"instanceName":"1"}),"instanceName":"1"}),"instanceName":"1"});
            var Q1508;
            Q1508=makeQuery(id+"F12.opPattern","COPY",BODY,{"derivedFrom":makeQuery(id+"F11.opPattern","COPY",BODY,{"derivedFrom":makeQuery(id+"F10.opPattern","COPY",BODY,{"derivedFrom":makeQuery(id+"F9.opPattern","COPY",BODY,{"derivedFrom":makeQuery(id+"F8.opPattern","COPY",BODY,{"derivedFrom":makeQuery(id+"F6.opPattern","COPY",BODY,{"derivedFrom":makeQuery(id+"F5.opPattern","COPY",BODY,{"derivedFrom":makeQuery(id+"F3.opPattern","COPY",BODY,{"derivedFrom":makeQuery(id+"F2.opPattern","COPY",BODY,{"derivedFrom":makeQuery(id+"F1.opRevolve","SWEPT_BODY",BODY,{"disambiguationData":[OSD([sQuery(id+"F0.wireOp",EDGE,"E1")])]}),"instanceName":"1"}),"instanceName":"1"}),"instanceName":"1"}),"instanceName":"1"}),"instanceName":"1"}),"instanceName":"1"}),"instanceName":"1"}),"instanceName":"1"}),"instanceName":"1"});
            var Q1509;
            Q1509=makeQuery(id+"F12.opPattern","COPY",BODY,{"derivedFrom":makeQuery(id+"F11.opPattern","COPY",BODY,{"derivedFrom":makeQuery(id+"F10.opPattern","COPY",BODY,{"derivedFrom":makeQuery(id+"F9.opPattern","COPY",BODY,{"derivedFrom":makeQuery(id+"F8.opPattern","COPY",BODY,{"derivedFrom":makeQuery(id+"F6.opPattern","COPY",BODY,{"derivedFrom":makeQuery(id+"F5.opPattern","COPY",BODY,{"derivedFrom":makeQuery(id+"F4.opPattern","COPY",BODY,{"derivedFrom":makeQuery(id+"F1.opRevolve","SWEPT_BODY",BODY,{"disambiguationData":[OSD([sQuery(id+"F0.wireOp",EDGE,"E1")])]}),"instanceName":"1"}),"instanceName":"1"}),"instanceName":"1"}),"instanceName":"1"}),"instanceName":"1"}),"instanceName":"1"}),"instanceName":"1"}),"instanceName":"1"});
            var Q1510;
            Q1510=makeQuery(id+"F12.opPattern","COPY",BODY,{"derivedFrom":makeQuery(id+"F11.opPattern","COPY",BODY,{"derivedFrom":makeQuery(id+"F10.opPattern","COPY",BODY,{"derivedFrom":makeQuery(id+"F9.opPattern","COPY",BODY,{"derivedFrom":makeQuery(id+"F8.opPattern","COPY",BODY,{"derivedFrom":makeQuery(id+"F6.opPattern","COPY",BODY,{"derivedFrom":makeQuery(id+"F5.opPattern","COPY",BODY,{"derivedFrom":makeQuery(id+"F4.opPattern","COPY",BODY,{"derivedFrom":makeQuery(id+"F2.opPattern","COPY",BODY,{"derivedFrom":makeQuery(id+"F1.opRevolve","SWEPT_BODY",BODY,{"disambiguationData":[OSD([sQuery(id+"F0.wireOp",EDGE,"E1")])]}),"instanceName":"1"}),"instanceName":"1"}),"instanceName":"1"}),"instanceName":"1"}),"instanceName":"1"}),"instanceName":"1"}),"instanceName":"1"}),"instanceName":"1"}),"instanceName":"1"});
            var Q1511;
            Q1511=makeQuery(id+"F12.opPattern","COPY",BODY,{"derivedFrom":makeQuery(id+"F11.opPattern","COPY",BODY,{"derivedFrom":makeQuery(id+"F10.opPattern","COPY",BODY,{"derivedFrom":makeQuery(id+"F9.opPattern","COPY",BODY,{"derivedFrom":makeQuery(id+"F8.opPattern","COPY",BODY,{"derivedFrom":makeQuery(id+"F6.opPattern","COPY",BODY,{"derivedFrom":makeQuery(id+"F5.opPattern","COPY",BODY,{"derivedFrom":makeQuery(id+"F4.opPattern","COPY",BODY,{"derivedFrom":makeQuery(id+"F3.opPattern","COPY",BODY,{"derivedFrom":makeQuery(id+"F2.opPattern","COPY",BODY,{"derivedFrom":makeQuery(id+"F1.opRevolve","SWEPT_BODY",BODY,{"disambiguationData":[OSD([sQuery(id+"F0.wireOp",EDGE,"E1")])]}),"instanceName":"1"}),"instanceName":"1"}),"instanceName":"1"}),"instanceName":"1"}),"instanceName":"1"}),"instanceName":"1"}),"instanceName":"1"}),"instanceName":"1"}),"instanceName":"1"}),"instanceName":"1"});
            var Q1512;
            Q1512=makeQuery(id+"F12.opPattern","COPY",BODY,{"derivedFrom":makeQuery(id+"F11.opPattern","COPY",BODY,{"derivedFrom":makeQuery(id+"F10.opPattern","COPY",BODY,{"derivedFrom":makeQuery(id+"F9.opPattern","COPY",BODY,{"derivedFrom":makeQuery(id+"F8.opPattern","COPY",BODY,{"derivedFrom":makeQuery(id+"F7.opPattern","COPY",BODY,{"derivedFrom":makeQuery(id+"F1.opRevolve","SWEPT_BODY",BODY,{"disambiguationData":[OSD([sQuery(id+"F0.wireOp",EDGE,"E1")])]}),"instanceName":"1"}),"instanceName":"1"}),"instanceName":"1"}),"instanceName":"1"}),"instanceName":"1"}),"instanceName":"1"});
            var Q1513;
            Q1513=makeQuery(id+"F12.opPattern","COPY",BODY,{"derivedFrom":makeQuery(id+"F11.opPattern","COPY",BODY,{"derivedFrom":makeQuery(id+"F10.opPattern","COPY",BODY,{"derivedFrom":makeQuery(id+"F9.opPattern","COPY",BODY,{"derivedFrom":makeQuery(id+"F8.opPattern","COPY",BODY,{"derivedFrom":makeQuery(id+"F7.opPattern","COPY",BODY,{"derivedFrom":makeQuery(id+"F2.opPattern","COPY",BODY,{"derivedFrom":makeQuery(id+"F1.opRevolve","SWEPT_BODY",BODY,{"disambiguationData":[OSD([sQuery(id+"F0.wireOp",EDGE,"E1")])]}),"instanceName":"1"}),"instanceName":"1"}),"instanceName":"1"}),"instanceName":"1"}),"instanceName":"1"}),"instanceName":"1"}),"instanceName":"1"});
            var Q1514;
            Q1514=makeQuery(id+"F12.opPattern","COPY",BODY,{"derivedFrom":makeQuery(id+"F11.opPattern","COPY",BODY,{"derivedFrom":makeQuery(id+"F10.opPattern","COPY",BODY,{"derivedFrom":makeQuery(id+"F9.opPattern","COPY",BODY,{"derivedFrom":makeQuery(id+"F8.opPattern","COPY",BODY,{"derivedFrom":makeQuery(id+"F7.opPattern","COPY",BODY,{"derivedFrom":makeQuery(id+"F3.opPattern","COPY",BODY,{"derivedFrom":makeQuery(id+"F2.opPattern","COPY",BODY,{"derivedFrom":makeQuery(id+"F1.opRevolve","SWEPT_BODY",BODY,{"disambiguationData":[OSD([sQuery(id+"F0.wireOp",EDGE,"E1")])]}),"instanceName":"1"}),"instanceName":"1"}),"instanceName":"1"}),"instanceName":"1"}),"instanceName":"1"}),"instanceName":"1"}),"instanceName":"1"}),"instanceName":"1"});
            var Q1515;
            Q1515=makeQuery(id+"F12.opPattern","COPY",BODY,{"derivedFrom":makeQuery(id+"F11.opPattern","COPY",BODY,{"derivedFrom":makeQuery(id+"F10.opPattern","COPY",BODY,{"derivedFrom":makeQuery(id+"F9.opPattern","COPY",BODY,{"derivedFrom":makeQuery(id+"F8.opPattern","COPY",BODY,{"derivedFrom":makeQuery(id+"F7.opPattern","COPY",BODY,{"derivedFrom":makeQuery(id+"F4.opPattern","COPY",BODY,{"derivedFrom":makeQuery(id+"F1.opRevolve","SWEPT_BODY",BODY,{"disambiguationData":[OSD([sQuery(id+"F0.wireOp",EDGE,"E1")])]}),"instanceName":"1"}),"instanceName":"1"}),"instanceName":"1"}),"instanceName":"1"}),"instanceName":"1"}),"instanceName":"1"}),"instanceName":"1"});
            var Q1516;
            Q1516=makeQuery(id+"F12.opPattern","COPY",BODY,{"derivedFrom":makeQuery(id+"F11.opPattern","COPY",BODY,{"derivedFrom":makeQuery(id+"F10.opPattern","COPY",BODY,{"derivedFrom":makeQuery(id+"F9.opPattern","COPY",BODY,{"derivedFrom":makeQuery(id+"F8.opPattern","COPY",BODY,{"derivedFrom":makeQuery(id+"F7.opPattern","COPY",BODY,{"derivedFrom":makeQuery(id+"F4.opPattern","COPY",BODY,{"derivedFrom":makeQuery(id+"F2.opPattern","COPY",BODY,{"derivedFrom":makeQuery(id+"F1.opRevolve","SWEPT_BODY",BODY,{"disambiguationData":[OSD([sQuery(id+"F0.wireOp",EDGE,"E1")])]}),"instanceName":"1"}),"instanceName":"1"}),"instanceName":"1"}),"instanceName":"1"}),"instanceName":"1"}),"instanceName":"1"}),"instanceName":"1"}),"instanceName":"1"});
            var Q1517;
            Q1517=makeQuery(id+"F12.opPattern","COPY",BODY,{"derivedFrom":makeQuery(id+"F11.opPattern","COPY",BODY,{"derivedFrom":makeQuery(id+"F10.opPattern","COPY",BODY,{"derivedFrom":makeQuery(id+"F9.opPattern","COPY",BODY,{"derivedFrom":makeQuery(id+"F8.opPattern","COPY",BODY,{"derivedFrom":makeQuery(id+"F7.opPattern","COPY",BODY,{"derivedFrom":makeQuery(id+"F4.opPattern","COPY",BODY,{"derivedFrom":makeQuery(id+"F3.opPattern","COPY",BODY,{"derivedFrom":makeQuery(id+"F2.opPattern","COPY",BODY,{"derivedFrom":makeQuery(id+"F1.opRevolve","SWEPT_BODY",BODY,{"disambiguationData":[OSD([sQuery(id+"F0.wireOp",EDGE,"E1")])]}),"instanceName":"1"}),"instanceName":"1"}),"instanceName":"1"}),"instanceName":"1"}),"instanceName":"1"}),"instanceName":"1"}),"instanceName":"1"}),"instanceName":"1"}),"instanceName":"1"});
            var Q1518;
            Q1518=makeQuery(id+"F12.opPattern","COPY",BODY,{"derivedFrom":makeQuery(id+"F11.opPattern","COPY",BODY,{"derivedFrom":makeQuery(id+"F10.opPattern","COPY",BODY,{"derivedFrom":makeQuery(id+"F9.opPattern","COPY",BODY,{"derivedFrom":makeQuery(id+"F8.opPattern","COPY",BODY,{"derivedFrom":makeQuery(id+"F7.opPattern","COPY",BODY,{"derivedFrom":makeQuery(id+"F5.opPattern","COPY",BODY,{"derivedFrom":makeQuery(id+"F1.opRevolve","SWEPT_BODY",BODY,{"disambiguationData":[OSD([sQuery(id+"F0.wireOp",EDGE,"E1")])]}),"instanceName":"1"}),"instanceName":"1"}),"instanceName":"1"}),"instanceName":"1"}),"instanceName":"1"}),"instanceName":"1"}),"instanceName":"1"});
            var Q1519;
            Q1519=makeQuery(id+"F12.opPattern","COPY",BODY,{"derivedFrom":makeQuery(id+"F11.opPattern","COPY",BODY,{"derivedFrom":makeQuery(id+"F10.opPattern","COPY",BODY,{"derivedFrom":makeQuery(id+"F9.opPattern","COPY",BODY,{"derivedFrom":makeQuery(id+"F8.opPattern","COPY",BODY,{"derivedFrom":makeQuery(id+"F7.opPattern","COPY",BODY,{"derivedFrom":makeQuery(id+"F5.opPattern","COPY",BODY,{"derivedFrom":makeQuery(id+"F2.opPattern","COPY",BODY,{"derivedFrom":makeQuery(id+"F1.opRevolve","SWEPT_BODY",BODY,{"disambiguationData":[OSD([sQuery(id+"F0.wireOp",EDGE,"E1")])]}),"instanceName":"1"}),"instanceName":"1"}),"instanceName":"1"}),"instanceName":"1"}),"instanceName":"1"}),"instanceName":"1"}),"instanceName":"1"}),"instanceName":"1"});
            var Q1520;
            Q1520=makeQuery(id+"F12.opPattern","COPY",BODY,{"derivedFrom":makeQuery(id+"F11.opPattern","COPY",BODY,{"derivedFrom":makeQuery(id+"F10.opPattern","COPY",BODY,{"derivedFrom":makeQuery(id+"F9.opPattern","COPY",BODY,{"derivedFrom":makeQuery(id+"F8.opPattern","COPY",BODY,{"derivedFrom":makeQuery(id+"F7.opPattern","COPY",BODY,{"derivedFrom":makeQuery(id+"F5.opPattern","COPY",BODY,{"derivedFrom":makeQuery(id+"F3.opPattern","COPY",BODY,{"derivedFrom":makeQuery(id+"F2.opPattern","COPY",BODY,{"derivedFrom":makeQuery(id+"F1.opRevolve","SWEPT_BODY",BODY,{"disambiguationData":[OSD([sQuery(id+"F0.wireOp",EDGE,"E1")])]}),"instanceName":"1"}),"instanceName":"1"}),"instanceName":"1"}),"instanceName":"1"}),"instanceName":"1"}),"instanceName":"1"}),"instanceName":"1"}),"instanceName":"1"}),"instanceName":"1"});
            var Q1521;
            Q1521=makeQuery(id+"F12.opPattern","COPY",BODY,{"derivedFrom":makeQuery(id+"F11.opPattern","COPY",BODY,{"derivedFrom":makeQuery(id+"F10.opPattern","COPY",BODY,{"derivedFrom":makeQuery(id+"F9.opPattern","COPY",BODY,{"derivedFrom":makeQuery(id+"F8.opPattern","COPY",BODY,{"derivedFrom":makeQuery(id+"F7.opPattern","COPY",BODY,{"derivedFrom":makeQuery(id+"F5.opPattern","COPY",BODY,{"derivedFrom":makeQuery(id+"F4.opPattern","COPY",BODY,{"derivedFrom":makeQuery(id+"F1.opRevolve","SWEPT_BODY",BODY,{"disambiguationData":[OSD([sQuery(id+"F0.wireOp",EDGE,"E1")])]}),"instanceName":"1"}),"instanceName":"1"}),"instanceName":"1"}),"instanceName":"1"}),"instanceName":"1"}),"instanceName":"1"}),"instanceName":"1"}),"instanceName":"1"});
            var Q1522;
            Q1522=makeQuery(id+"F12.opPattern","COPY",BODY,{"derivedFrom":makeQuery(id+"F11.opPattern","COPY",BODY,{"derivedFrom":makeQuery(id+"F10.opPattern","COPY",BODY,{"derivedFrom":makeQuery(id+"F9.opPattern","COPY",BODY,{"derivedFrom":makeQuery(id+"F8.opPattern","COPY",BODY,{"derivedFrom":makeQuery(id+"F7.opPattern","COPY",BODY,{"derivedFrom":makeQuery(id+"F5.opPattern","COPY",BODY,{"derivedFrom":makeQuery(id+"F4.opPattern","COPY",BODY,{"derivedFrom":makeQuery(id+"F2.opPattern","COPY",BODY,{"derivedFrom":makeQuery(id+"F1.opRevolve","SWEPT_BODY",BODY,{"disambiguationData":[OSD([sQuery(id+"F0.wireOp",EDGE,"E1")])]}),"instanceName":"1"}),"instanceName":"1"}),"instanceName":"1"}),"instanceName":"1"}),"instanceName":"1"}),"instanceName":"1"}),"instanceName":"1"}),"instanceName":"1"}),"instanceName":"1"});
            var Q1523;
            Q1523=makeQuery(id+"F12.opPattern","COPY",BODY,{"derivedFrom":makeQuery(id+"F11.opPattern","COPY",BODY,{"derivedFrom":makeQuery(id+"F10.opPattern","COPY",BODY,{"derivedFrom":makeQuery(id+"F9.opPattern","COPY",BODY,{"derivedFrom":makeQuery(id+"F8.opPattern","COPY",BODY,{"derivedFrom":makeQuery(id+"F7.opPattern","COPY",BODY,{"derivedFrom":makeQuery(id+"F5.opPattern","COPY",BODY,{"derivedFrom":makeQuery(id+"F4.opPattern","COPY",BODY,{"derivedFrom":makeQuery(id+"F3.opPattern","COPY",BODY,{"derivedFrom":makeQuery(id+"F2.opPattern","COPY",BODY,{"derivedFrom":makeQuery(id+"F1.opRevolve","SWEPT_BODY",BODY,{"disambiguationData":[OSD([sQuery(id+"F0.wireOp",EDGE,"E1")])]}),"instanceName":"1"}),"instanceName":"1"}),"instanceName":"1"}),"instanceName":"1"}),"instanceName":"1"}),"instanceName":"1"}),"instanceName":"1"}),"instanceName":"1"}),"instanceName":"1"}),"instanceName":"1"});
            var Q1524;
            Q1524=makeQuery(id+"F12.opPattern","COPY",BODY,{"derivedFrom":makeQuery(id+"F11.opPattern","COPY",BODY,{"derivedFrom":makeQuery(id+"F10.opPattern","COPY",BODY,{"derivedFrom":makeQuery(id+"F9.opPattern","COPY",BODY,{"derivedFrom":makeQuery(id+"F8.opPattern","COPY",BODY,{"derivedFrom":makeQuery(id+"F7.opPattern","COPY",BODY,{"derivedFrom":makeQuery(id+"F6.opPattern","COPY",BODY,{"derivedFrom":makeQuery(id+"F1.opRevolve","SWEPT_BODY",BODY,{"disambiguationData":[OSD([sQuery(id+"F0.wireOp",EDGE,"E1")])]}),"instanceName":"1"}),"instanceName":"1"}),"instanceName":"1"}),"instanceName":"1"}),"instanceName":"1"}),"instanceName":"1"}),"instanceName":"1"});
            var Q1525;
            Q1525=makeQuery(id+"F12.opPattern","COPY",BODY,{"derivedFrom":makeQuery(id+"F11.opPattern","COPY",BODY,{"derivedFrom":makeQuery(id+"F10.opPattern","COPY",BODY,{"derivedFrom":makeQuery(id+"F9.opPattern","COPY",BODY,{"derivedFrom":makeQuery(id+"F8.opPattern","COPY",BODY,{"derivedFrom":makeQuery(id+"F7.opPattern","COPY",BODY,{"derivedFrom":makeQuery(id+"F6.opPattern","COPY",BODY,{"derivedFrom":makeQuery(id+"F2.opPattern","COPY",BODY,{"derivedFrom":makeQuery(id+"F1.opRevolve","SWEPT_BODY",BODY,{"disambiguationData":[OSD([sQuery(id+"F0.wireOp",EDGE,"E1")])]}),"instanceName":"1"}),"instanceName":"1"}),"instanceName":"1"}),"instanceName":"1"}),"instanceName":"1"}),"instanceName":"1"}),"instanceName":"1"}),"instanceName":"1"});
            var Q1526;
            Q1526=makeQuery(id+"F12.opPattern","COPY",BODY,{"derivedFrom":makeQuery(id+"F11.opPattern","COPY",BODY,{"derivedFrom":makeQuery(id+"F10.opPattern","COPY",BODY,{"derivedFrom":makeQuery(id+"F9.opPattern","COPY",BODY,{"derivedFrom":makeQuery(id+"F8.opPattern","COPY",BODY,{"derivedFrom":makeQuery(id+"F7.opPattern","COPY",BODY,{"derivedFrom":makeQuery(id+"F6.opPattern","COPY",BODY,{"derivedFrom":makeQuery(id+"F3.opPattern","COPY",BODY,{"derivedFrom":makeQuery(id+"F2.opPattern","COPY",BODY,{"derivedFrom":makeQuery(id+"F1.opRevolve","SWEPT_BODY",BODY,{"disambiguationData":[OSD([sQuery(id+"F0.wireOp",EDGE,"E1")])]}),"instanceName":"1"}),"instanceName":"1"}),"instanceName":"1"}),"instanceName":"1"}),"instanceName":"1"}),"instanceName":"1"}),"instanceName":"1"}),"instanceName":"1"}),"instanceName":"1"});
            var Q1527;
            Q1527=makeQuery(id+"F12.opPattern","COPY",BODY,{"derivedFrom":makeQuery(id+"F11.opPattern","COPY",BODY,{"derivedFrom":makeQuery(id+"F10.opPattern","COPY",BODY,{"derivedFrom":makeQuery(id+"F9.opPattern","COPY",BODY,{"derivedFrom":makeQuery(id+"F8.opPattern","COPY",BODY,{"derivedFrom":makeQuery(id+"F7.opPattern","COPY",BODY,{"derivedFrom":makeQuery(id+"F6.opPattern","COPY",BODY,{"derivedFrom":makeQuery(id+"F4.opPattern","COPY",BODY,{"derivedFrom":makeQuery(id+"F1.opRevolve","SWEPT_BODY",BODY,{"disambiguationData":[OSD([sQuery(id+"F0.wireOp",EDGE,"E1")])]}),"instanceName":"1"}),"instanceName":"1"}),"instanceName":"1"}),"instanceName":"1"}),"instanceName":"1"}),"instanceName":"1"}),"instanceName":"1"}),"instanceName":"1"});
            var Q1528;
            Q1528=makeQuery(id+"F12.opPattern","COPY",BODY,{"derivedFrom":makeQuery(id+"F11.opPattern","COPY",BODY,{"derivedFrom":makeQuery(id+"F10.opPattern","COPY",BODY,{"derivedFrom":makeQuery(id+"F9.opPattern","COPY",BODY,{"derivedFrom":makeQuery(id+"F8.opPattern","COPY",BODY,{"derivedFrom":makeQuery(id+"F7.opPattern","COPY",BODY,{"derivedFrom":makeQuery(id+"F6.opPattern","COPY",BODY,{"derivedFrom":makeQuery(id+"F4.opPattern","COPY",BODY,{"derivedFrom":makeQuery(id+"F2.opPattern","COPY",BODY,{"derivedFrom":makeQuery(id+"F1.opRevolve","SWEPT_BODY",BODY,{"disambiguationData":[OSD([sQuery(id+"F0.wireOp",EDGE,"E1")])]}),"instanceName":"1"}),"instanceName":"1"}),"instanceName":"1"}),"instanceName":"1"}),"instanceName":"1"}),"instanceName":"1"}),"instanceName":"1"}),"instanceName":"1"}),"instanceName":"1"});
            var Q1529;
            Q1529=makeQuery(id+"F12.opPattern","COPY",BODY,{"derivedFrom":makeQuery(id+"F11.opPattern","COPY",BODY,{"derivedFrom":makeQuery(id+"F10.opPattern","COPY",BODY,{"derivedFrom":makeQuery(id+"F9.opPattern","COPY",BODY,{"derivedFrom":makeQuery(id+"F8.opPattern","COPY",BODY,{"derivedFrom":makeQuery(id+"F7.opPattern","COPY",BODY,{"derivedFrom":makeQuery(id+"F6.opPattern","COPY",BODY,{"derivedFrom":makeQuery(id+"F4.opPattern","COPY",BODY,{"derivedFrom":makeQuery(id+"F3.opPattern","COPY",BODY,{"derivedFrom":makeQuery(id+"F2.opPattern","COPY",BODY,{"derivedFrom":makeQuery(id+"F1.opRevolve","SWEPT_BODY",BODY,{"disambiguationData":[OSD([sQuery(id+"F0.wireOp",EDGE,"E1")])]}),"instanceName":"1"}),"instanceName":"1"}),"instanceName":"1"}),"instanceName":"1"}),"instanceName":"1"}),"instanceName":"1"}),"instanceName":"1"}),"instanceName":"1"}),"instanceName":"1"}),"instanceName":"1"});
            var Q1530;
            Q1530=makeQuery(id+"F12.opPattern","COPY",BODY,{"derivedFrom":makeQuery(id+"F11.opPattern","COPY",BODY,{"derivedFrom":makeQuery(id+"F10.opPattern","COPY",BODY,{"derivedFrom":makeQuery(id+"F9.opPattern","COPY",BODY,{"derivedFrom":makeQuery(id+"F8.opPattern","COPY",BODY,{"derivedFrom":makeQuery(id+"F7.opPattern","COPY",BODY,{"derivedFrom":makeQuery(id+"F6.opPattern","COPY",BODY,{"derivedFrom":makeQuery(id+"F5.opPattern","COPY",BODY,{"derivedFrom":makeQuery(id+"F1.opRevolve","SWEPT_BODY",BODY,{"disambiguationData":[OSD([sQuery(id+"F0.wireOp",EDGE,"E1")])]}),"instanceName":"1"}),"instanceName":"1"}),"instanceName":"1"}),"instanceName":"1"}),"instanceName":"1"}),"instanceName":"1"}),"instanceName":"1"}),"instanceName":"1"});
            var Q1531;
            Q1531=makeQuery(id+"F12.opPattern","COPY",BODY,{"derivedFrom":makeQuery(id+"F11.opPattern","COPY",BODY,{"derivedFrom":makeQuery(id+"F10.opPattern","COPY",BODY,{"derivedFrom":makeQuery(id+"F9.opPattern","COPY",BODY,{"derivedFrom":makeQuery(id+"F8.opPattern","COPY",BODY,{"derivedFrom":makeQuery(id+"F7.opPattern","COPY",BODY,{"derivedFrom":makeQuery(id+"F6.opPattern","COPY",BODY,{"derivedFrom":makeQuery(id+"F5.opPattern","COPY",BODY,{"derivedFrom":makeQuery(id+"F2.opPattern","COPY",BODY,{"derivedFrom":makeQuery(id+"F1.opRevolve","SWEPT_BODY",BODY,{"disambiguationData":[OSD([sQuery(id+"F0.wireOp",EDGE,"E1")])]}),"instanceName":"1"}),"instanceName":"1"}),"instanceName":"1"}),"instanceName":"1"}),"instanceName":"1"}),"instanceName":"1"}),"instanceName":"1"}),"instanceName":"1"}),"instanceName":"1"});
            var Q1532;
            Q1532=makeQuery(id+"F12.opPattern","COPY",BODY,{"derivedFrom":makeQuery(id+"F11.opPattern","COPY",BODY,{"derivedFrom":makeQuery(id+"F10.opPattern","COPY",BODY,{"derivedFrom":makeQuery(id+"F9.opPattern","COPY",BODY,{"derivedFrom":makeQuery(id+"F8.opPattern","COPY",BODY,{"derivedFrom":makeQuery(id+"F7.opPattern","COPY",BODY,{"derivedFrom":makeQuery(id+"F6.opPattern","COPY",BODY,{"derivedFrom":makeQuery(id+"F5.opPattern","COPY",BODY,{"derivedFrom":makeQuery(id+"F3.opPattern","COPY",BODY,{"derivedFrom":makeQuery(id+"F2.opPattern","COPY",BODY,{"derivedFrom":makeQuery(id+"F1.opRevolve","SWEPT_BODY",BODY,{"disambiguationData":[OSD([sQuery(id+"F0.wireOp",EDGE,"E1")])]}),"instanceName":"1"}),"instanceName":"1"}),"instanceName":"1"}),"instanceName":"1"}),"instanceName":"1"}),"instanceName":"1"}),"instanceName":"1"}),"instanceName":"1"}),"instanceName":"1"}),"instanceName":"1"});
            var Q1533;
            Q1533=makeQuery(id+"F12.opPattern","COPY",BODY,{"derivedFrom":makeQuery(id+"F11.opPattern","COPY",BODY,{"derivedFrom":makeQuery(id+"F10.opPattern","COPY",BODY,{"derivedFrom":makeQuery(id+"F9.opPattern","COPY",BODY,{"derivedFrom":makeQuery(id+"F8.opPattern","COPY",BODY,{"derivedFrom":makeQuery(id+"F7.opPattern","COPY",BODY,{"derivedFrom":makeQuery(id+"F6.opPattern","COPY",BODY,{"derivedFrom":makeQuery(id+"F5.opPattern","COPY",BODY,{"derivedFrom":makeQuery(id+"F4.opPattern","COPY",BODY,{"derivedFrom":makeQuery(id+"F1.opRevolve","SWEPT_BODY",BODY,{"disambiguationData":[OSD([sQuery(id+"F0.wireOp",EDGE,"E1")])]}),"instanceName":"1"}),"instanceName":"1"}),"instanceName":"1"}),"instanceName":"1"}),"instanceName":"1"}),"instanceName":"1"}),"instanceName":"1"}),"instanceName":"1"}),"instanceName":"1"});
            var Q1534;
            Q1534=makeQuery(id+"F12.opPattern","COPY",BODY,{"derivedFrom":makeQuery(id+"F11.opPattern","COPY",BODY,{"derivedFrom":makeQuery(id+"F10.opPattern","COPY",BODY,{"derivedFrom":makeQuery(id+"F9.opPattern","COPY",BODY,{"derivedFrom":makeQuery(id+"F8.opPattern","COPY",BODY,{"derivedFrom":makeQuery(id+"F7.opPattern","COPY",BODY,{"derivedFrom":makeQuery(id+"F6.opPattern","COPY",BODY,{"derivedFrom":makeQuery(id+"F5.opPattern","COPY",BODY,{"derivedFrom":makeQuery(id+"F4.opPattern","COPY",BODY,{"derivedFrom":makeQuery(id+"F2.opPattern","COPY",BODY,{"derivedFrom":makeQuery(id+"F1.opRevolve","SWEPT_BODY",BODY,{"disambiguationData":[OSD([sQuery(id+"F0.wireOp",EDGE,"E1")])]}),"instanceName":"1"}),"instanceName":"1"}),"instanceName":"1"}),"instanceName":"1"}),"instanceName":"1"}),"instanceName":"1"}),"instanceName":"1"}),"instanceName":"1"}),"instanceName":"1"}),"instanceName":"1"});
            var Q1535;
            Q1535=makeQuery(id+"F12.opPattern","COPY",BODY,{"derivedFrom":makeQuery(id+"F11.opPattern","COPY",BODY,{"derivedFrom":makeQuery(id+"F10.opPattern","COPY",BODY,{"derivedFrom":makeQuery(id+"F9.opPattern","COPY",BODY,{"derivedFrom":makeQuery(id+"F8.opPattern","COPY",BODY,{"derivedFrom":makeQuery(id+"F7.opPattern","COPY",BODY,{"derivedFrom":makeQuery(id+"F6.opPattern","COPY",BODY,{"derivedFrom":makeQuery(id+"F5.opPattern","COPY",BODY,{"derivedFrom":makeQuery(id+"F4.opPattern","COPY",BODY,{"derivedFrom":makeQuery(id+"F3.opPattern","COPY",BODY,{"derivedFrom":makeQuery(id+"F2.opPattern","COPY",BODY,{"derivedFrom":makeQuery(id+"F1.opRevolve","SWEPT_BODY",BODY,{"disambiguationData":[OSD([sQuery(id+"F0.wireOp",EDGE,"E1")])]}),"instanceName":"1"}),"instanceName":"1"}),"instanceName":"1"}),"instanceName":"1"}),"instanceName":"1"}),"instanceName":"1"}),"instanceName":"1"}),"instanceName":"1"}),"instanceName":"1"}),"instanceName":"1"}),"instanceName":"1"});
            transform(context, id + "F13", {"entities" : qUnion([Q0, Q1, Q2, Q3, Q4, Q5, Q6, Q7, Q8, Q9, Q10, Q11, Q12, Q13, Q14, Q15, Q16, Q17, Q18, Q19, Q20, Q21, Q22, Q23, Q24, Q25, Q26, Q27, Q28, Q29, Q30, Q31, Q32, Q33, Q34, Q35, Q36, Q37, Q38, Q39, Q40, Q41, Q42, Q43, Q44, Q45, Q46, Q47, Q48, Q49, Q50, Q51, Q52, Q53, Q54, Q55, Q56, Q57, Q58, Q59, Q60, Q61, Q62, Q63, Q64, Q65, Q66, Q67, Q68, Q69, Q70, Q71, Q72, Q73, Q74, Q75, Q76, Q77, Q78, Q79, Q80, Q81, Q82, Q83, Q84, Q85, Q86, Q87, Q88, Q89, Q90, Q91, Q92, Q93, Q94, Q95, Q96, Q97, Q98, Q99, Q100, Q101, Q102, Q103, Q104, Q105, Q106, Q107, Q108, Q109, Q110, Q111, Q112, Q113, Q114, Q115, Q116, Q117, Q118, Q119, Q120, Q121, Q122, Q123, Q124, Q125, Q126, Q127, Q128, Q129, Q130, Q131, Q132, Q133, Q134, Q135, Q136, Q137, Q138, Q139, Q140, Q141, Q142, Q143, Q144, Q145, Q146, Q147, Q148, Q149, Q150, Q151, Q152, Q153, Q154, Q155, Q156, Q157, Q158, Q159, Q160, Q161, Q162, Q163, Q164, Q165, Q166, Q167, Q168, Q169, Q170, Q171, Q172, Q173, Q174, Q175, Q176, Q177, Q178, Q179, Q180, Q181, Q182, Q183, Q184, Q185, Q186, Q187, Q188, Q189, Q190, Q191, Q192, Q193, Q194, Q195, Q196, Q197, Q198, Q199, Q200, Q201, Q202, Q203, Q204, Q205, Q206, Q207, Q208, Q209, Q210, Q211, Q212, Q213, Q214, Q215, Q216, Q217, Q218, Q219, Q220, Q221, Q222, Q223, Q224, Q225, Q226, Q227, Q228, Q229, Q230, Q231, Q232, Q233, Q234, Q235, Q236, Q237, Q238, Q239, Q240, Q241, Q242, Q243, Q244, Q245, Q246, Q247, Q248, Q249, Q250, Q251, Q252, Q253, Q254, Q255, Q256, Q257, Q258, Q259, Q260, Q261, Q262, Q263, Q264, Q265, Q266, Q267, Q268, Q269, Q270, Q271, Q272, Q273, Q274, Q275, Q276, Q277, Q278, Q279, Q280, Q281, Q282, Q283, Q284, Q285, Q286, Q287, Q288, Q289, Q290, Q291, Q292, Q293, Q294, Q295, Q296, Q297, Q298, Q299, Q300, Q301, Q302, Q303, Q304, Q305, Q306, Q307, Q308, Q309, Q310, Q311, Q312, Q313, Q314, Q315, Q316, Q317, Q318, Q319, Q320, Q321, Q322, Q323, Q324, Q325, Q326, Q327, Q328, Q329, Q330, Q331, Q332, Q333, Q334, Q335, Q336, Q337, Q338, Q339, Q340, Q341, Q342, Q343, Q344, Q345, Q346, Q347, Q348, Q349, Q350, Q351, Q352, Q353, Q354, Q355, Q356, Q357, Q358, Q359, Q360, Q361, Q362, Q363, Q364, Q365, Q366, Q367, Q368, Q369, Q370, Q371, Q372, Q373, Q374, Q375, Q376, Q377, Q378, Q379, Q380, Q381, Q382, Q383, Q384, Q385, Q386, Q387, Q388, Q389, Q390, Q391, Q392, Q393, Q394, Q395, Q396, Q397, Q398, Q399, Q400, Q401, Q402, Q403, Q404, Q405, Q406, Q407, Q408, Q409, Q410, Q411, Q412, Q413, Q414, Q415, Q416, Q417, Q418, Q419, Q420, Q421, Q422, Q423, Q424, Q425, Q426, Q427, Q428, Q429, Q430, Q431, Q432, Q433, Q434, Q435, Q436, Q437, Q438, Q439, Q440, Q441, Q442, Q443, Q444, Q445, Q446, Q447, Q448, Q449, Q450, Q451, Q452, Q453, Q454, Q455, Q456, Q457, Q458, Q459, Q460, Q461, Q462, Q463, Q464, Q465, Q466, Q467, Q468, Q469, Q470, Q471, Q472, Q473, Q474, Q475, Q476, Q477, Q478, Q479, Q480, Q481, Q482, Q483, Q484, Q485, Q486, Q487, Q488, Q489, Q490, Q491, Q492, Q493, Q494, Q495, Q496, Q497, Q498, Q499, Q500, Q501, Q502, Q503, Q504, Q505, Q506, Q507, Q508, Q509, Q510, Q511, Q512, Q513, Q514, Q515, Q516, Q517, Q518, Q519, Q520, Q521, Q522, Q523, Q524, Q525, Q526, Q527, Q528, Q529, Q530, Q531, Q532, Q533, Q534, Q535, Q536, Q537, Q538, Q539, Q540, Q541, Q542, Q543, Q544, Q545, Q546, Q547, Q548, Q549, Q550, Q551, Q552, Q553, Q554, Q555, Q556, Q557, Q558, Q559, Q560, Q561, Q562, Q563, Q564, Q565, Q566, Q567, Q568, Q569, Q570, Q571, Q572, Q573, Q574, Q575, Q576, Q577, Q578, Q579, Q580, Q581, Q582, Q583, Q584, Q585, Q586, Q587, Q588, Q589, Q590, Q591, Q592, Q593, Q594, Q595, Q596, Q597, Q598, Q599, Q600, Q601, Q602, Q603, Q604, Q605, Q606, Q607, Q608, Q609, Q610, Q611, Q612, Q613, Q614, Q615, Q616, Q617, Q618, Q619, Q620, Q621, Q622, Q623, Q624, Q625, Q626, Q627, Q628, Q629, Q630, Q631, Q632, Q633, Q634, Q635, Q636, Q637, Q638, Q639, Q640, Q641, Q642, Q643, Q644, Q645, Q646, Q647, Q648, Q649, Q650, Q651, Q652, Q653, Q654, Q655, Q656, Q657, Q658, Q659, Q660, Q661, Q662, Q663, Q664, Q665, Q666, Q667, Q668, Q669, Q670, Q671, Q672, Q673, Q674, Q675, Q676, Q677, Q678, Q679, Q680, Q681, Q682, Q683, Q684, Q685, Q686, Q687, Q688, Q689, Q690, Q691, Q692, Q693, Q694, Q695, Q696, Q697, Q698, Q699, Q700, Q701, Q702, Q703, Q704, Q705, Q706, Q707, Q708, Q709, Q710, Q711, Q712, Q713, Q714, Q715, Q716, Q717, Q718, Q719, Q720, Q721, Q722, Q723, Q724, Q725, Q726, Q727, Q728, Q729, Q730, Q731, Q732, Q733, Q734, Q735, Q736, Q737, Q738, Q739, Q740, Q741, Q742, Q743, Q744, Q745, Q746, Q747, Q748, Q749, Q750, Q751, Q752, Q753, Q754, Q755, Q756, Q757, Q758, Q759, Q760, Q761, Q762, Q763, Q764, Q765, Q766, Q767, Q768, Q769, Q770, Q771, Q772, Q773, Q774, Q775, Q776, Q777, Q778, Q779, Q780, Q781, Q782, Q783, Q784, Q785, Q786, Q787, Q788, Q789, Q790, Q791, Q792, Q793, Q794, Q795, Q796, Q797, Q798, Q799, Q800, Q801, Q802, Q803, Q804, Q805, Q806, Q807, Q808, Q809, Q810, Q811, Q812, Q813, Q814, Q815, Q816, Q817, Q818, Q819, Q820, Q821, Q822, Q823, Q824, Q825, Q826, Q827, Q828, Q829, Q830, Q831, Q832, Q833, Q834, Q835, Q836, Q837, Q838, Q839, Q840, Q841, Q842, Q843, Q844, Q845, Q846, Q847, Q848, Q849, Q850, Q851, Q852, Q853, Q854, Q855, Q856, Q857, Q858, Q859, Q860, Q861, Q862, Q863, Q864, Q865, Q866, Q867, Q868, Q869, Q870, Q871, Q872, Q873, Q874, Q875, Q876, Q877, Q878, Q879, Q880, Q881, Q882, Q883, Q884, Q885, Q886, Q887, Q888, Q889, Q890, Q891, Q892, Q893, Q894, Q895, Q896, Q897, Q898, Q899, Q900, Q901, Q902, Q903, Q904, Q905, Q906, Q907, Q908, Q909, Q910, Q911, Q912, Q913, Q914, Q915, Q916, Q917, Q918, Q919, Q920, Q921, Q922, Q923, Q924, Q925, Q926, Q927, Q928, Q929, Q930, Q931, Q932, Q933, Q934, Q935, Q936, Q937, Q938, Q939, Q940, Q941, Q942, Q943, Q944, Q945, Q946, Q947, Q948, Q949, Q950, Q951, Q952, Q953, Q954, Q955, Q956, Q957, Q958, Q959, Q960, Q961, Q962, Q963, Q964, Q965, Q966, Q967, Q968, Q969, Q970, Q971, Q972, Q973, Q974, Q975, Q976, Q977, Q978, Q979, Q980, Q981, Q982, Q983, Q984, Q985, Q986, Q987, Q988, Q989, Q990, Q991, Q992, Q993, Q994, Q995, Q996, Q997, Q998, Q999, Q1000, Q1001, Q1002, Q1003, Q1004, Q1005, Q1006, Q1007, Q1008, Q1009, Q1010, Q1011, Q1012, Q1013, Q1014, Q1015, Q1016, Q1017, Q1018, Q1019, Q1020, Q1021, Q1022, Q1023, Q1024, Q1025, Q1026, Q1027, Q1028, Q1029, Q1030, Q1031, Q1032, Q1033, Q1034, Q1035, Q1036, Q1037, Q1038, Q1039, Q1040, Q1041, Q1042, Q1043, Q1044, Q1045, Q1046, Q1047, Q1048, Q1049, Q1050, Q1051, Q1052, Q1053, Q1054, Q1055, Q1056, Q1057, Q1058, Q1059, Q1060, Q1061, Q1062, Q1063, Q1064, Q1065, Q1066, Q1067, Q1068, Q1069, Q1070, Q1071, Q1072, Q1073, Q1074, Q1075, Q1076, Q1077, Q1078, Q1079, Q1080, Q1081, Q1082, Q1083, Q1084, Q1085, Q1086, Q1087, Q1088, Q1089, Q1090, Q1091, Q1092, Q1093, Q1094, Q1095, Q1096, Q1097, Q1098, Q1099, Q1100, Q1101, Q1102, Q1103, Q1104, Q1105, Q1106, Q1107, Q1108, Q1109, Q1110, Q1111, Q1112, Q1113, Q1114, Q1115, Q1116, Q1117, Q1118, Q1119, Q1120, Q1121, Q1122, Q1123, Q1124, Q1125, Q1126, Q1127, Q1128, Q1129, Q1130, Q1131, Q1132, Q1133, Q1134, Q1135, Q1136, Q1137, Q1138, Q1139, Q1140, Q1141, Q1142, Q1143, Q1144, Q1145, Q1146, Q1147, Q1148, Q1149, Q1150, Q1151, Q1152, Q1153, Q1154, Q1155, Q1156, Q1157, Q1158, Q1159, Q1160, Q1161, Q1162, Q1163, Q1164, Q1165, Q1166, Q1167, Q1168, Q1169, Q1170, Q1171, Q1172, Q1173, Q1174, Q1175, Q1176, Q1177, Q1178, Q1179, Q1180, Q1181, Q1182, Q1183, Q1184, Q1185, Q1186, Q1187, Q1188, Q1189, Q1190, Q1191, Q1192, Q1193, Q1194, Q1195, Q1196, Q1197, Q1198, Q1199, Q1200, Q1201, Q1202, Q1203, Q1204, Q1205, Q1206, Q1207, Q1208, Q1209, Q1210, Q1211, Q1212, Q1213, Q1214, Q1215, Q1216, Q1217, Q1218, Q1219, Q1220, Q1221, Q1222, Q1223, Q1224, Q1225, Q1226, Q1227, Q1228, Q1229, Q1230, Q1231, Q1232, Q1233, Q1234, Q1235, Q1236, Q1237, Q1238, Q1239, Q1240, Q1241, Q1242, Q1243, Q1244, Q1245, Q1246, Q1247, Q1248, Q1249, Q1250, Q1251, Q1252, Q1253, Q1254, Q1255, Q1256, Q1257, Q1258, Q1259, Q1260, Q1261, Q1262, Q1263, Q1264, Q1265, Q1266, Q1267, Q1268, Q1269, Q1270, Q1271, Q1272, Q1273, Q1274, Q1275, Q1276, Q1277, Q1278, Q1279, Q1280, Q1281, Q1282, Q1283, Q1284, Q1285, Q1286, Q1287, Q1288, Q1289, Q1290, Q1291, Q1292, Q1293, Q1294, Q1295, Q1296, Q1297, Q1298, Q1299, Q1300, Q1301, Q1302, Q1303, Q1304, Q1305, Q1306, Q1307, Q1308, Q1309, Q1310, Q1311, Q1312, Q1313, Q1314, Q1315, Q1316, Q1317, Q1318, Q1319, Q1320, Q1321, Q1322, Q1323, Q1324, Q1325, Q1326, Q1327, Q1328, Q1329, Q1330, Q1331, Q1332, Q1333, Q1334, Q1335, Q1336, Q1337, Q1338, Q1339, Q1340, Q1341, Q1342, Q1343, Q1344, Q1345, Q1346, Q1347, Q1348, Q1349, Q1350, Q1351, Q1352, Q1353, Q1354, Q1355, Q1356, Q1357, Q1358, Q1359, Q1360, Q1361, Q1362, Q1363, Q1364, Q1365, Q1366, Q1367, Q1368, Q1369, Q1370, Q1371, Q1372, Q1373, Q1374, Q1375, Q1376, Q1377, Q1378, Q1379, Q1380, Q1381, Q1382, Q1383, Q1384, Q1385, Q1386, Q1387, Q1388, Q1389, Q1390, Q1391, Q1392, Q1393, Q1394, Q1395, Q1396, Q1397, Q1398, Q1399, Q1400, Q1401, Q1402, Q1403, Q1404, Q1405, Q1406, Q1407, Q1408, Q1409, Q1410, Q1411, Q1412, Q1413, Q1414, Q1415, Q1416, Q1417, Q1418, Q1419, Q1420, Q1421, Q1422, Q1423, Q1424, Q1425, Q1426, Q1427, Q1428, Q1429, Q1430, Q1431, Q1432, Q1433, Q1434, Q1435, Q1436, Q1437, Q1438, Q1439, Q1440, Q1441, Q1442, Q1443, Q1444, Q1445, Q1446, Q1447, Q1448, Q1449, Q1450, Q1451, Q1452, Q1453, Q1454, Q1455, Q1456, Q1457, Q1458, Q1459, Q1460, Q1461, Q1462, Q1463, Q1464, Q1465, Q1466, Q1467, Q1468, Q1469, Q1470, Q1471, Q1472, Q1473, Q1474, Q1475, Q1476, Q1477, Q1478, Q1479, Q1480, Q1481, Q1482, Q1483, Q1484, Q1485, Q1486, Q1487, Q1488, Q1489, Q1490, Q1491, Q1492, Q1493, Q1494, Q1495, Q1496, Q1497, Q1498, Q1499, Q1500, Q1501, Q1502, Q1503, Q1504, Q1505, Q1506, Q1507, Q1508, Q1509, Q1510, Q1511, Q1512, Q1513, Q1514, Q1515, Q1516, Q1517, Q1518, Q1519, Q1520, Q1521, Q1522, Q1523, Q1524, Q1525, Q1526, Q1527, Q1528, Q1529, Q1530, Q1531, Q1532, Q1533, Q1534, Q1535]), "transformType" : TransformType.TRANSLATION_3D, "dx" : 0 * mm, "dy" : 1.12 * mm, "dz" : 0 * mm, "makeCopy" : true});
        }
        {
            var Q0;
            Q0=makeQuery(id+"F2.opPattern","COPY",BODY,{"derivedFrom":makeQuery(id+"F1.opRevolve","SWEPT_BODY",BODY,{"disambiguationData":[OSD([sQuery(id+"F0.wireOp",EDGE,"E1")])]}),"instanceName":"1"});
            var Q1;
            Q1=makeQuery(id+"F3.opPattern","COPY",BODY,{"derivedFrom":makeQuery(id+"F2.opPattern","COPY",BODY,{"derivedFrom":makeQuery(id+"F1.opRevolve","SWEPT_BODY",BODY,{"disambiguationData":[OSD([sQuery(id+"F0.wireOp",EDGE,"E1")])]}),"instanceName":"1"}),"instanceName":"1"});
            var Q2;
            Q2=makeQuery(id+"F4.opPattern","COPY",BODY,{"derivedFrom":makeQuery(id+"F1.opRevolve","SWEPT_BODY",BODY,{"disambiguationData":[OSD([sQuery(id+"F0.wireOp",EDGE,"E1")])]}),"instanceName":"1"});
            var Q3;
            Q3=makeQuery(id+"F4.opPattern","COPY",BODY,{"derivedFrom":makeQuery(id+"F2.opPattern","COPY",BODY,{"derivedFrom":makeQuery(id+"F1.opRevolve","SWEPT_BODY",BODY,{"disambiguationData":[OSD([sQuery(id+"F0.wireOp",EDGE,"E1")])]}),"instanceName":"1"}),"instanceName":"1"});
            var Q4;
            Q4=makeQuery(id+"F4.opPattern","COPY",BODY,{"derivedFrom":makeQuery(id+"F3.opPattern","COPY",BODY,{"derivedFrom":makeQuery(id+"F2.opPattern","COPY",BODY,{"derivedFrom":makeQuery(id+"F1.opRevolve","SWEPT_BODY",BODY,{"disambiguationData":[OSD([sQuery(id+"F0.wireOp",EDGE,"E1")])]}),"instanceName":"1"}),"instanceName":"1"}),"instanceName":"1"});
            var Q5;
            Q5=makeQuery(id+"F5.opPattern","COPY",BODY,{"derivedFrom":makeQuery(id+"F1.opRevolve","SWEPT_BODY",BODY,{"disambiguationData":[OSD([sQuery(id+"F0.wireOp",EDGE,"E1")])]}),"instanceName":"1"});
            var Q6;
            Q6=makeQuery(id+"F5.opPattern","COPY",BODY,{"derivedFrom":makeQuery(id+"F2.opPattern","COPY",BODY,{"derivedFrom":makeQuery(id+"F1.opRevolve","SWEPT_BODY",BODY,{"disambiguationData":[OSD([sQuery(id+"F0.wireOp",EDGE,"E1")])]}),"instanceName":"1"}),"instanceName":"1"});
            var Q7;
            Q7=makeQuery(id+"F5.opPattern","COPY",BODY,{"derivedFrom":makeQuery(id+"F3.opPattern","COPY",BODY,{"derivedFrom":makeQuery(id+"F2.opPattern","COPY",BODY,{"derivedFrom":makeQuery(id+"F1.opRevolve","SWEPT_BODY",BODY,{"disambiguationData":[OSD([sQuery(id+"F0.wireOp",EDGE,"E1")])]}),"instanceName":"1"}),"instanceName":"1"}),"instanceName":"1"});
            var Q8;
            Q8=makeQuery(id+"F5.opPattern","COPY",BODY,{"derivedFrom":makeQuery(id+"F4.opPattern","COPY",BODY,{"derivedFrom":makeQuery(id+"F1.opRevolve","SWEPT_BODY",BODY,{"disambiguationData":[OSD([sQuery(id+"F0.wireOp",EDGE,"E1")])]}),"instanceName":"1"}),"instanceName":"1"});
            var Q9;
            Q9=makeQuery(id+"F5.opPattern","COPY",BODY,{"derivedFrom":makeQuery(id+"F4.opPattern","COPY",BODY,{"derivedFrom":makeQuery(id+"F2.opPattern","COPY",BODY,{"derivedFrom":makeQuery(id+"F1.opRevolve","SWEPT_BODY",BODY,{"disambiguationData":[OSD([sQuery(id+"F0.wireOp",EDGE,"E1")])]}),"instanceName":"1"}),"instanceName":"1"}),"instanceName":"1"});
            var Q10;
            Q10=makeQuery(id+"F5.opPattern","COPY",BODY,{"derivedFrom":makeQuery(id+"F4.opPattern","COPY",BODY,{"derivedFrom":makeQuery(id+"F3.opPattern","COPY",BODY,{"derivedFrom":makeQuery(id+"F2.opPattern","COPY",BODY,{"derivedFrom":makeQuery(id+"F1.opRevolve","SWEPT_BODY",BODY,{"disambiguationData":[OSD([sQuery(id+"F0.wireOp",EDGE,"E1")])]}),"instanceName":"1"}),"instanceName":"1"}),"instanceName":"1"}),"instanceName":"1"});
            var Q11;
            Q11=makeQuery(id+"F6.opPattern","COPY",BODY,{"derivedFrom":makeQuery(id+"F1.opRevolve","SWEPT_BODY",BODY,{"disambiguationData":[OSD([sQuery(id+"F0.wireOp",EDGE,"E1")])]}),"instanceName":"1"});
            var Q12;
            Q12=makeQuery(id+"F6.opPattern","COPY",BODY,{"derivedFrom":makeQuery(id+"F2.opPattern","COPY",BODY,{"derivedFrom":makeQuery(id+"F1.opRevolve","SWEPT_BODY",BODY,{"disambiguationData":[OSD([sQuery(id+"F0.wireOp",EDGE,"E1")])]}),"instanceName":"1"}),"instanceName":"1"});
            var Q13;
            Q13=makeQuery(id+"F6.opPattern","COPY",BODY,{"derivedFrom":makeQuery(id+"F3.opPattern","COPY",BODY,{"derivedFrom":makeQuery(id+"F2.opPattern","COPY",BODY,{"derivedFrom":makeQuery(id+"F1.opRevolve","SWEPT_BODY",BODY,{"disambiguationData":[OSD([sQuery(id+"F0.wireOp",EDGE,"E1")])]}),"instanceName":"1"}),"instanceName":"1"}),"instanceName":"1"});
            var Q14;
            Q14=makeQuery(id+"F6.opPattern","COPY",BODY,{"derivedFrom":makeQuery(id+"F4.opPattern","COPY",BODY,{"derivedFrom":makeQuery(id+"F1.opRevolve","SWEPT_BODY",BODY,{"disambiguationData":[OSD([sQuery(id+"F0.wireOp",EDGE,"E1")])]}),"instanceName":"1"}),"instanceName":"1"});
            var Q15;
            Q15=makeQuery(id+"F6.opPattern","COPY",BODY,{"derivedFrom":makeQuery(id+"F4.opPattern","COPY",BODY,{"derivedFrom":makeQuery(id+"F2.opPattern","COPY",BODY,{"derivedFrom":makeQuery(id+"F1.opRevolve","SWEPT_BODY",BODY,{"disambiguationData":[OSD([sQuery(id+"F0.wireOp",EDGE,"E1")])]}),"instanceName":"1"}),"instanceName":"1"}),"instanceName":"1"});
            var Q16;
            Q16=makeQuery(id+"F6.opPattern","COPY",BODY,{"derivedFrom":makeQuery(id+"F4.opPattern","COPY",BODY,{"derivedFrom":makeQuery(id+"F3.opPattern","COPY",BODY,{"derivedFrom":makeQuery(id+"F2.opPattern","COPY",BODY,{"derivedFrom":makeQuery(id+"F1.opRevolve","SWEPT_BODY",BODY,{"disambiguationData":[OSD([sQuery(id+"F0.wireOp",EDGE,"E1")])]}),"instanceName":"1"}),"instanceName":"1"}),"instanceName":"1"}),"instanceName":"1"});
            var Q17;
            Q17=makeQuery(id+"F6.opPattern","COPY",BODY,{"derivedFrom":makeQuery(id+"F5.opPattern","COPY",BODY,{"derivedFrom":makeQuery(id+"F1.opRevolve","SWEPT_BODY",BODY,{"disambiguationData":[OSD([sQuery(id+"F0.wireOp",EDGE,"E1")])]}),"instanceName":"1"}),"instanceName":"1"});
            var Q18;
            Q18=makeQuery(id+"F6.opPattern","COPY",BODY,{"derivedFrom":makeQuery(id+"F5.opPattern","COPY",BODY,{"derivedFrom":makeQuery(id+"F2.opPattern","COPY",BODY,{"derivedFrom":makeQuery(id+"F1.opRevolve","SWEPT_BODY",BODY,{"disambiguationData":[OSD([sQuery(id+"F0.wireOp",EDGE,"E1")])]}),"instanceName":"1"}),"instanceName":"1"}),"instanceName":"1"});
            var Q19;
            Q19=makeQuery(id+"F6.opPattern","COPY",BODY,{"derivedFrom":makeQuery(id+"F5.opPattern","COPY",BODY,{"derivedFrom":makeQuery(id+"F3.opPattern","COPY",BODY,{"derivedFrom":makeQuery(id+"F2.opPattern","COPY",BODY,{"derivedFrom":makeQuery(id+"F1.opRevolve","SWEPT_BODY",BODY,{"disambiguationData":[OSD([sQuery(id+"F0.wireOp",EDGE,"E1")])]}),"instanceName":"1"}),"instanceName":"1"}),"instanceName":"1"}),"instanceName":"1"});
            var Q20;
            Q20=makeQuery(id+"F6.opPattern","COPY",BODY,{"derivedFrom":makeQuery(id+"F5.opPattern","COPY",BODY,{"derivedFrom":makeQuery(id+"F4.opPattern","COPY",BODY,{"derivedFrom":makeQuery(id+"F1.opRevolve","SWEPT_BODY",BODY,{"disambiguationData":[OSD([sQuery(id+"F0.wireOp",EDGE,"E1")])]}),"instanceName":"1"}),"instanceName":"1"}),"instanceName":"1"});
            var Q21;
            Q21=makeQuery(id+"F6.opPattern","COPY",BODY,{"derivedFrom":makeQuery(id+"F5.opPattern","COPY",BODY,{"derivedFrom":makeQuery(id+"F4.opPattern","COPY",BODY,{"derivedFrom":makeQuery(id+"F2.opPattern","COPY",BODY,{"derivedFrom":makeQuery(id+"F1.opRevolve","SWEPT_BODY",BODY,{"disambiguationData":[OSD([sQuery(id+"F0.wireOp",EDGE,"E1")])]}),"instanceName":"1"}),"instanceName":"1"}),"instanceName":"1"}),"instanceName":"1"});
            var Q22;
            Q22=makeQuery(id+"F6.opPattern","COPY",BODY,{"derivedFrom":makeQuery(id+"F5.opPattern","COPY",BODY,{"derivedFrom":makeQuery(id+"F4.opPattern","COPY",BODY,{"derivedFrom":makeQuery(id+"F3.opPattern","COPY",BODY,{"derivedFrom":makeQuery(id+"F2.opPattern","COPY",BODY,{"derivedFrom":makeQuery(id+"F1.opRevolve","SWEPT_BODY",BODY,{"disambiguationData":[OSD([sQuery(id+"F0.wireOp",EDGE,"E1")])]}),"instanceName":"1"}),"instanceName":"1"}),"instanceName":"1"}),"instanceName":"1"}),"instanceName":"1"});
            var Q23;
            Q23=makeQuery(id+"F7.opPattern","COPY",BODY,{"derivedFrom":makeQuery(id+"F1.opRevolve","SWEPT_BODY",BODY,{"disambiguationData":[OSD([sQuery(id+"F0.wireOp",EDGE,"E1")])]}),"instanceName":"1"});
            var Q24;
            Q24=makeQuery(id+"F7.opPattern","COPY",BODY,{"derivedFrom":makeQuery(id+"F2.opPattern","COPY",BODY,{"derivedFrom":makeQuery(id+"F1.opRevolve","SWEPT_BODY",BODY,{"disambiguationData":[OSD([sQuery(id+"F0.wireOp",EDGE,"E1")])]}),"instanceName":"1"}),"instanceName":"1"});
            var Q25;
            Q25=makeQuery(id+"F7.opPattern","COPY",BODY,{"derivedFrom":makeQuery(id+"F3.opPattern","COPY",BODY,{"derivedFrom":makeQuery(id+"F2.opPattern","COPY",BODY,{"derivedFrom":makeQuery(id+"F1.opRevolve","SWEPT_BODY",BODY,{"disambiguationData":[OSD([sQuery(id+"F0.wireOp",EDGE,"E1")])]}),"instanceName":"1"}),"instanceName":"1"}),"instanceName":"1"});
            var Q26;
            Q26=makeQuery(id+"F7.opPattern","COPY",BODY,{"derivedFrom":makeQuery(id+"F4.opPattern","COPY",BODY,{"derivedFrom":makeQuery(id+"F1.opRevolve","SWEPT_BODY",BODY,{"disambiguationData":[OSD([sQuery(id+"F0.wireOp",EDGE,"E1")])]}),"instanceName":"1"}),"instanceName":"1"});
            var Q27;
            Q27=makeQuery(id+"F7.opPattern","COPY",BODY,{"derivedFrom":makeQuery(id+"F4.opPattern","COPY",BODY,{"derivedFrom":makeQuery(id+"F2.opPattern","COPY",BODY,{"derivedFrom":makeQuery(id+"F1.opRevolve","SWEPT_BODY",BODY,{"disambiguationData":[OSD([sQuery(id+"F0.wireOp",EDGE,"E1")])]}),"instanceName":"1"}),"instanceName":"1"}),"instanceName":"1"});
            var Q28;
            Q28=makeQuery(id+"F7.opPattern","COPY",BODY,{"derivedFrom":makeQuery(id+"F4.opPattern","COPY",BODY,{"derivedFrom":makeQuery(id+"F3.opPattern","COPY",BODY,{"derivedFrom":makeQuery(id+"F2.opPattern","COPY",BODY,{"derivedFrom":makeQuery(id+"F1.opRevolve","SWEPT_BODY",BODY,{"disambiguationData":[OSD([sQuery(id+"F0.wireOp",EDGE,"E1")])]}),"instanceName":"1"}),"instanceName":"1"}),"instanceName":"1"}),"instanceName":"1"});
            var Q29;
            Q29=makeQuery(id+"F7.opPattern","COPY",BODY,{"derivedFrom":makeQuery(id+"F5.opPattern","COPY",BODY,{"derivedFrom":makeQuery(id+"F1.opRevolve","SWEPT_BODY",BODY,{"disambiguationData":[OSD([sQuery(id+"F0.wireOp",EDGE,"E1")])]}),"instanceName":"1"}),"instanceName":"1"});
            var Q30;
            Q30=makeQuery(id+"F7.opPattern","COPY",BODY,{"derivedFrom":makeQuery(id+"F5.opPattern","COPY",BODY,{"derivedFrom":makeQuery(id+"F2.opPattern","COPY",BODY,{"derivedFrom":makeQuery(id+"F1.opRevolve","SWEPT_BODY",BODY,{"disambiguationData":[OSD([sQuery(id+"F0.wireOp",EDGE,"E1")])]}),"instanceName":"1"}),"instanceName":"1"}),"instanceName":"1"});
            var Q31;
            Q31=makeQuery(id+"F7.opPattern","COPY",BODY,{"derivedFrom":makeQuery(id+"F5.opPattern","COPY",BODY,{"derivedFrom":makeQuery(id+"F3.opPattern","COPY",BODY,{"derivedFrom":makeQuery(id+"F2.opPattern","COPY",BODY,{"derivedFrom":makeQuery(id+"F1.opRevolve","SWEPT_BODY",BODY,{"disambiguationData":[OSD([sQuery(id+"F0.wireOp",EDGE,"E1")])]}),"instanceName":"1"}),"instanceName":"1"}),"instanceName":"1"}),"instanceName":"1"});
            var Q32;
            Q32=makeQuery(id+"F7.opPattern","COPY",BODY,{"derivedFrom":makeQuery(id+"F5.opPattern","COPY",BODY,{"derivedFrom":makeQuery(id+"F4.opPattern","COPY",BODY,{"derivedFrom":makeQuery(id+"F1.opRevolve","SWEPT_BODY",BODY,{"disambiguationData":[OSD([sQuery(id+"F0.wireOp",EDGE,"E1")])]}),"instanceName":"1"}),"instanceName":"1"}),"instanceName":"1"});
            var Q33;
            Q33=makeQuery(id+"F7.opPattern","COPY",BODY,{"derivedFrom":makeQuery(id+"F5.opPattern","COPY",BODY,{"derivedFrom":makeQuery(id+"F4.opPattern","COPY",BODY,{"derivedFrom":makeQuery(id+"F2.opPattern","COPY",BODY,{"derivedFrom":makeQuery(id+"F1.opRevolve","SWEPT_BODY",BODY,{"disambiguationData":[OSD([sQuery(id+"F0.wireOp",EDGE,"E1")])]}),"instanceName":"1"}),"instanceName":"1"}),"instanceName":"1"}),"instanceName":"1"});
            var Q34;
            Q34=makeQuery(id+"F7.opPattern","COPY",BODY,{"derivedFrom":makeQuery(id+"F5.opPattern","COPY",BODY,{"derivedFrom":makeQuery(id+"F4.opPattern","COPY",BODY,{"derivedFrom":makeQuery(id+"F3.opPattern","COPY",BODY,{"derivedFrom":makeQuery(id+"F2.opPattern","COPY",BODY,{"derivedFrom":makeQuery(id+"F1.opRevolve","SWEPT_BODY",BODY,{"disambiguationData":[OSD([sQuery(id+"F0.wireOp",EDGE,"E1")])]}),"instanceName":"1"}),"instanceName":"1"}),"instanceName":"1"}),"instanceName":"1"}),"instanceName":"1"});
            var Q35;
            Q35=makeQuery(id+"F7.opPattern","COPY",BODY,{"derivedFrom":makeQuery(id+"F6.opPattern","COPY",BODY,{"derivedFrom":makeQuery(id+"F1.opRevolve","SWEPT_BODY",BODY,{"disambiguationData":[OSD([sQuery(id+"F0.wireOp",EDGE,"E1")])]}),"instanceName":"1"}),"instanceName":"1"});
            var Q36;
            Q36=makeQuery(id+"F7.opPattern","COPY",BODY,{"derivedFrom":makeQuery(id+"F6.opPattern","COPY",BODY,{"derivedFrom":makeQuery(id+"F2.opPattern","COPY",BODY,{"derivedFrom":makeQuery(id+"F1.opRevolve","SWEPT_BODY",BODY,{"disambiguationData":[OSD([sQuery(id+"F0.wireOp",EDGE,"E1")])]}),"instanceName":"1"}),"instanceName":"1"}),"instanceName":"1"});
            var Q37;
            Q37=makeQuery(id+"F7.opPattern","COPY",BODY,{"derivedFrom":makeQuery(id+"F6.opPattern","COPY",BODY,{"derivedFrom":makeQuery(id+"F3.opPattern","COPY",BODY,{"derivedFrom":makeQuery(id+"F2.opPattern","COPY",BODY,{"derivedFrom":makeQuery(id+"F1.opRevolve","SWEPT_BODY",BODY,{"disambiguationData":[OSD([sQuery(id+"F0.wireOp",EDGE,"E1")])]}),"instanceName":"1"}),"instanceName":"1"}),"instanceName":"1"}),"instanceName":"1"});
            var Q38;
            Q38=makeQuery(id+"F7.opPattern","COPY",BODY,{"derivedFrom":makeQuery(id+"F6.opPattern","COPY",BODY,{"derivedFrom":makeQuery(id+"F4.opPattern","COPY",BODY,{"derivedFrom":makeQuery(id+"F1.opRevolve","SWEPT_BODY",BODY,{"disambiguationData":[OSD([sQuery(id+"F0.wireOp",EDGE,"E1")])]}),"instanceName":"1"}),"instanceName":"1"}),"instanceName":"1"});
            var Q39;
            Q39=makeQuery(id+"F7.opPattern","COPY",BODY,{"derivedFrom":makeQuery(id+"F6.opPattern","COPY",BODY,{"derivedFrom":makeQuery(id+"F4.opPattern","COPY",BODY,{"derivedFrom":makeQuery(id+"F2.opPattern","COPY",BODY,{"derivedFrom":makeQuery(id+"F1.opRevolve","SWEPT_BODY",BODY,{"disambiguationData":[OSD([sQuery(id+"F0.wireOp",EDGE,"E1")])]}),"instanceName":"1"}),"instanceName":"1"}),"instanceName":"1"}),"instanceName":"1"});
            var Q40;
            Q40=makeQuery(id+"F7.opPattern","COPY",BODY,{"derivedFrom":makeQuery(id+"F6.opPattern","COPY",BODY,{"derivedFrom":makeQuery(id+"F4.opPattern","COPY",BODY,{"derivedFrom":makeQuery(id+"F3.opPattern","COPY",BODY,{"derivedFrom":makeQuery(id+"F2.opPattern","COPY",BODY,{"derivedFrom":makeQuery(id+"F1.opRevolve","SWEPT_BODY",BODY,{"disambiguationData":[OSD([sQuery(id+"F0.wireOp",EDGE,"E1")])]}),"instanceName":"1"}),"instanceName":"1"}),"instanceName":"1"}),"instanceName":"1"}),"instanceName":"1"});
            var Q41;
            Q41=makeQuery(id+"F7.opPattern","COPY",BODY,{"derivedFrom":makeQuery(id+"F6.opPattern","COPY",BODY,{"derivedFrom":makeQuery(id+"F5.opPattern","COPY",BODY,{"derivedFrom":makeQuery(id+"F1.opRevolve","SWEPT_BODY",BODY,{"disambiguationData":[OSD([sQuery(id+"F0.wireOp",EDGE,"E1")])]}),"instanceName":"1"}),"instanceName":"1"}),"instanceName":"1"});
            var Q42;
            Q42=makeQuery(id+"F7.opPattern","COPY",BODY,{"derivedFrom":makeQuery(id+"F6.opPattern","COPY",BODY,{"derivedFrom":makeQuery(id+"F5.opPattern","COPY",BODY,{"derivedFrom":makeQuery(id+"F2.opPattern","COPY",BODY,{"derivedFrom":makeQuery(id+"F1.opRevolve","SWEPT_BODY",BODY,{"disambiguationData":[OSD([sQuery(id+"F0.wireOp",EDGE,"E1")])]}),"instanceName":"1"}),"instanceName":"1"}),"instanceName":"1"}),"instanceName":"1"});
            var Q43;
            Q43=makeQuery(id+"F7.opPattern","COPY",BODY,{"derivedFrom":makeQuery(id+"F6.opPattern","COPY",BODY,{"derivedFrom":makeQuery(id+"F5.opPattern","COPY",BODY,{"derivedFrom":makeQuery(id+"F3.opPattern","COPY",BODY,{"derivedFrom":makeQuery(id+"F2.opPattern","COPY",BODY,{"derivedFrom":makeQuery(id+"F1.opRevolve","SWEPT_BODY",BODY,{"disambiguationData":[OSD([sQuery(id+"F0.wireOp",EDGE,"E1")])]}),"instanceName":"1"}),"instanceName":"1"}),"instanceName":"1"}),"instanceName":"1"}),"instanceName":"1"});
            var Q44;
            Q44=makeQuery(id+"F7.opPattern","COPY",BODY,{"derivedFrom":makeQuery(id+"F6.opPattern","COPY",BODY,{"derivedFrom":makeQuery(id+"F5.opPattern","COPY",BODY,{"derivedFrom":makeQuery(id+"F4.opPattern","COPY",BODY,{"derivedFrom":makeQuery(id+"F1.opRevolve","SWEPT_BODY",BODY,{"disambiguationData":[OSD([sQuery(id+"F0.wireOp",EDGE,"E1")])]}),"instanceName":"1"}),"instanceName":"1"}),"instanceName":"1"}),"instanceName":"1"});
            var Q45;
            Q45=makeQuery(id+"F7.opPattern","COPY",BODY,{"derivedFrom":makeQuery(id+"F6.opPattern","COPY",BODY,{"derivedFrom":makeQuery(id+"F5.opPattern","COPY",BODY,{"derivedFrom":makeQuery(id+"F4.opPattern","COPY",BODY,{"derivedFrom":makeQuery(id+"F2.opPattern","COPY",BODY,{"derivedFrom":makeQuery(id+"F1.opRevolve","SWEPT_BODY",BODY,{"disambiguationData":[OSD([sQuery(id+"F0.wireOp",EDGE,"E1")])]}),"instanceName":"1"}),"instanceName":"1"}),"instanceName":"1"}),"instanceName":"1"}),"instanceName":"1"});
            var Q46;
            Q46=makeQuery(id+"F7.opPattern","COPY",BODY,{"derivedFrom":makeQuery(id+"F6.opPattern","COPY",BODY,{"derivedFrom":makeQuery(id+"F5.opPattern","COPY",BODY,{"derivedFrom":makeQuery(id+"F4.opPattern","COPY",BODY,{"derivedFrom":makeQuery(id+"F3.opPattern","COPY",BODY,{"derivedFrom":makeQuery(id+"F2.opPattern","COPY",BODY,{"derivedFrom":makeQuery(id+"F1.opRevolve","SWEPT_BODY",BODY,{"disambiguationData":[OSD([sQuery(id+"F0.wireOp",EDGE,"E1")])]}),"instanceName":"1"}),"instanceName":"1"}),"instanceName":"1"}),"instanceName":"1"}),"instanceName":"1"}),"instanceName":"1"});
            var Q47;
            Q47=makeQuery(id+"F8.opPattern","COPY",BODY,{"derivedFrom":makeQuery(id+"F1.opRevolve","SWEPT_BODY",BODY,{"disambiguationData":[OSD([sQuery(id+"F0.wireOp",EDGE,"E1")])]}),"instanceName":"1"});
            var Q48;
            Q48=makeQuery(id+"F8.opPattern","COPY",BODY,{"derivedFrom":makeQuery(id+"F2.opPattern","COPY",BODY,{"derivedFrom":makeQuery(id+"F1.opRevolve","SWEPT_BODY",BODY,{"disambiguationData":[OSD([sQuery(id+"F0.wireOp",EDGE,"E1")])]}),"instanceName":"1"}),"instanceName":"1"});
            var Q49;
            Q49=makeQuery(id+"F8.opPattern","COPY",BODY,{"derivedFrom":makeQuery(id+"F3.opPattern","COPY",BODY,{"derivedFrom":makeQuery(id+"F2.opPattern","COPY",BODY,{"derivedFrom":makeQuery(id+"F1.opRevolve","SWEPT_BODY",BODY,{"disambiguationData":[OSD([sQuery(id+"F0.wireOp",EDGE,"E1")])]}),"instanceName":"1"}),"instanceName":"1"}),"instanceName":"1"});
            var Q50;
            Q50=makeQuery(id+"F8.opPattern","COPY",BODY,{"derivedFrom":makeQuery(id+"F4.opPattern","COPY",BODY,{"derivedFrom":makeQuery(id+"F1.opRevolve","SWEPT_BODY",BODY,{"disambiguationData":[OSD([sQuery(id+"F0.wireOp",EDGE,"E1")])]}),"instanceName":"1"}),"instanceName":"1"});
            var Q51;
            Q51=makeQuery(id+"F8.opPattern","COPY",BODY,{"derivedFrom":makeQuery(id+"F4.opPattern","COPY",BODY,{"derivedFrom":makeQuery(id+"F2.opPattern","COPY",BODY,{"derivedFrom":makeQuery(id+"F1.opRevolve","SWEPT_BODY",BODY,{"disambiguationData":[OSD([sQuery(id+"F0.wireOp",EDGE,"E1")])]}),"instanceName":"1"}),"instanceName":"1"}),"instanceName":"1"});
            var Q52;
            Q52=makeQuery(id+"F8.opPattern","COPY",BODY,{"derivedFrom":makeQuery(id+"F4.opPattern","COPY",BODY,{"derivedFrom":makeQuery(id+"F3.opPattern","COPY",BODY,{"derivedFrom":makeQuery(id+"F2.opPattern","COPY",BODY,{"derivedFrom":makeQuery(id+"F1.opRevolve","SWEPT_BODY",BODY,{"disambiguationData":[OSD([sQuery(id+"F0.wireOp",EDGE,"E1")])]}),"instanceName":"1"}),"instanceName":"1"}),"instanceName":"1"}),"instanceName":"1"});
            var Q53;
            Q53=makeQuery(id+"F8.opPattern","COPY",BODY,{"derivedFrom":makeQuery(id+"F5.opPattern","COPY",BODY,{"derivedFrom":makeQuery(id+"F1.opRevolve","SWEPT_BODY",BODY,{"disambiguationData":[OSD([sQuery(id+"F0.wireOp",EDGE,"E1")])]}),"instanceName":"1"}),"instanceName":"1"});
            var Q54;
            Q54=makeQuery(id+"F8.opPattern","COPY",BODY,{"derivedFrom":makeQuery(id+"F5.opPattern","COPY",BODY,{"derivedFrom":makeQuery(id+"F2.opPattern","COPY",BODY,{"derivedFrom":makeQuery(id+"F1.opRevolve","SWEPT_BODY",BODY,{"disambiguationData":[OSD([sQuery(id+"F0.wireOp",EDGE,"E1")])]}),"instanceName":"1"}),"instanceName":"1"}),"instanceName":"1"});
            var Q55;
            Q55=makeQuery(id+"F8.opPattern","COPY",BODY,{"derivedFrom":makeQuery(id+"F5.opPattern","COPY",BODY,{"derivedFrom":makeQuery(id+"F3.opPattern","COPY",BODY,{"derivedFrom":makeQuery(id+"F2.opPattern","COPY",BODY,{"derivedFrom":makeQuery(id+"F1.opRevolve","SWEPT_BODY",BODY,{"disambiguationData":[OSD([sQuery(id+"F0.wireOp",EDGE,"E1")])]}),"instanceName":"1"}),"instanceName":"1"}),"instanceName":"1"}),"instanceName":"1"});
            var Q56;
            Q56=makeQuery(id+"F8.opPattern","COPY",BODY,{"derivedFrom":makeQuery(id+"F5.opPattern","COPY",BODY,{"derivedFrom":makeQuery(id+"F4.opPattern","COPY",BODY,{"derivedFrom":makeQuery(id+"F1.opRevolve","SWEPT_BODY",BODY,{"disambiguationData":[OSD([sQuery(id+"F0.wireOp",EDGE,"E1")])]}),"instanceName":"1"}),"instanceName":"1"}),"instanceName":"1"});
            var Q57;
            Q57=makeQuery(id+"F8.opPattern","COPY",BODY,{"derivedFrom":makeQuery(id+"F5.opPattern","COPY",BODY,{"derivedFrom":makeQuery(id+"F4.opPattern","COPY",BODY,{"derivedFrom":makeQuery(id+"F2.opPattern","COPY",BODY,{"derivedFrom":makeQuery(id+"F1.opRevolve","SWEPT_BODY",BODY,{"disambiguationData":[OSD([sQuery(id+"F0.wireOp",EDGE,"E1")])]}),"instanceName":"1"}),"instanceName":"1"}),"instanceName":"1"}),"instanceName":"1"});
            var Q58;
            Q58=makeQuery(id+"F8.opPattern","COPY",BODY,{"derivedFrom":makeQuery(id+"F5.opPattern","COPY",BODY,{"derivedFrom":makeQuery(id+"F4.opPattern","COPY",BODY,{"derivedFrom":makeQuery(id+"F3.opPattern","COPY",BODY,{"derivedFrom":makeQuery(id+"F2.opPattern","COPY",BODY,{"derivedFrom":makeQuery(id+"F1.opRevolve","SWEPT_BODY",BODY,{"disambiguationData":[OSD([sQuery(id+"F0.wireOp",EDGE,"E1")])]}),"instanceName":"1"}),"instanceName":"1"}),"instanceName":"1"}),"instanceName":"1"}),"instanceName":"1"});
            var Q59;
            Q59=makeQuery(id+"F8.opPattern","COPY",BODY,{"derivedFrom":makeQuery(id+"F6.opPattern","COPY",BODY,{"derivedFrom":makeQuery(id+"F1.opRevolve","SWEPT_BODY",BODY,{"disambiguationData":[OSD([sQuery(id+"F0.wireOp",EDGE,"E1")])]}),"instanceName":"1"}),"instanceName":"1"});
            var Q60;
            Q60=makeQuery(id+"F8.opPattern","COPY",BODY,{"derivedFrom":makeQuery(id+"F6.opPattern","COPY",BODY,{"derivedFrom":makeQuery(id+"F2.opPattern","COPY",BODY,{"derivedFrom":makeQuery(id+"F1.opRevolve","SWEPT_BODY",BODY,{"disambiguationData":[OSD([sQuery(id+"F0.wireOp",EDGE,"E1")])]}),"instanceName":"1"}),"instanceName":"1"}),"instanceName":"1"});
            var Q61;
            Q61=makeQuery(id+"F8.opPattern","COPY",BODY,{"derivedFrom":makeQuery(id+"F6.opPattern","COPY",BODY,{"derivedFrom":makeQuery(id+"F3.opPattern","COPY",BODY,{"derivedFrom":makeQuery(id+"F2.opPattern","COPY",BODY,{"derivedFrom":makeQuery(id+"F1.opRevolve","SWEPT_BODY",BODY,{"disambiguationData":[OSD([sQuery(id+"F0.wireOp",EDGE,"E1")])]}),"instanceName":"1"}),"instanceName":"1"}),"instanceName":"1"}),"instanceName":"1"});
            var Q62;
            Q62=makeQuery(id+"F8.opPattern","COPY",BODY,{"derivedFrom":makeQuery(id+"F6.opPattern","COPY",BODY,{"derivedFrom":makeQuery(id+"F4.opPattern","COPY",BODY,{"derivedFrom":makeQuery(id+"F1.opRevolve","SWEPT_BODY",BODY,{"disambiguationData":[OSD([sQuery(id+"F0.wireOp",EDGE,"E1")])]}),"instanceName":"1"}),"instanceName":"1"}),"instanceName":"1"});
            var Q63;
            Q63=makeQuery(id+"F8.opPattern","COPY",BODY,{"derivedFrom":makeQuery(id+"F6.opPattern","COPY",BODY,{"derivedFrom":makeQuery(id+"F4.opPattern","COPY",BODY,{"derivedFrom":makeQuery(id+"F2.opPattern","COPY",BODY,{"derivedFrom":makeQuery(id+"F1.opRevolve","SWEPT_BODY",BODY,{"disambiguationData":[OSD([sQuery(id+"F0.wireOp",EDGE,"E1")])]}),"instanceName":"1"}),"instanceName":"1"}),"instanceName":"1"}),"instanceName":"1"});
            var Q64;
            Q64=makeQuery(id+"F8.opPattern","COPY",BODY,{"derivedFrom":makeQuery(id+"F6.opPattern","COPY",BODY,{"derivedFrom":makeQuery(id+"F4.opPattern","COPY",BODY,{"derivedFrom":makeQuery(id+"F3.opPattern","COPY",BODY,{"derivedFrom":makeQuery(id+"F2.opPattern","COPY",BODY,{"derivedFrom":makeQuery(id+"F1.opRevolve","SWEPT_BODY",BODY,{"disambiguationData":[OSD([sQuery(id+"F0.wireOp",EDGE,"E1")])]}),"instanceName":"1"}),"instanceName":"1"}),"instanceName":"1"}),"instanceName":"1"}),"instanceName":"1"});
            var Q65;
            Q65=makeQuery(id+"F8.opPattern","COPY",BODY,{"derivedFrom":makeQuery(id+"F6.opPattern","COPY",BODY,{"derivedFrom":makeQuery(id+"F5.opPattern","COPY",BODY,{"derivedFrom":makeQuery(id+"F1.opRevolve","SWEPT_BODY",BODY,{"disambiguationData":[OSD([sQuery(id+"F0.wireOp",EDGE,"E1")])]}),"instanceName":"1"}),"instanceName":"1"}),"instanceName":"1"});
            var Q66;
            Q66=makeQuery(id+"F8.opPattern","COPY",BODY,{"derivedFrom":makeQuery(id+"F6.opPattern","COPY",BODY,{"derivedFrom":makeQuery(id+"F5.opPattern","COPY",BODY,{"derivedFrom":makeQuery(id+"F2.opPattern","COPY",BODY,{"derivedFrom":makeQuery(id+"F1.opRevolve","SWEPT_BODY",BODY,{"disambiguationData":[OSD([sQuery(id+"F0.wireOp",EDGE,"E1")])]}),"instanceName":"1"}),"instanceName":"1"}),"instanceName":"1"}),"instanceName":"1"});
            var Q67;
            Q67=makeQuery(id+"F8.opPattern","COPY",BODY,{"derivedFrom":makeQuery(id+"F6.opPattern","COPY",BODY,{"derivedFrom":makeQuery(id+"F5.opPattern","COPY",BODY,{"derivedFrom":makeQuery(id+"F3.opPattern","COPY",BODY,{"derivedFrom":makeQuery(id+"F2.opPattern","COPY",BODY,{"derivedFrom":makeQuery(id+"F1.opRevolve","SWEPT_BODY",BODY,{"disambiguationData":[OSD([sQuery(id+"F0.wireOp",EDGE,"E1")])]}),"instanceName":"1"}),"instanceName":"1"}),"instanceName":"1"}),"instanceName":"1"}),"instanceName":"1"});
            var Q68;
            Q68=makeQuery(id+"F8.opPattern","COPY",BODY,{"derivedFrom":makeQuery(id+"F6.opPattern","COPY",BODY,{"derivedFrom":makeQuery(id+"F5.opPattern","COPY",BODY,{"derivedFrom":makeQuery(id+"F4.opPattern","COPY",BODY,{"derivedFrom":makeQuery(id+"F1.opRevolve","SWEPT_BODY",BODY,{"disambiguationData":[OSD([sQuery(id+"F0.wireOp",EDGE,"E1")])]}),"instanceName":"1"}),"instanceName":"1"}),"instanceName":"1"}),"instanceName":"1"});
            var Q69;
            Q69=makeQuery(id+"F8.opPattern","COPY",BODY,{"derivedFrom":makeQuery(id+"F6.opPattern","COPY",BODY,{"derivedFrom":makeQuery(id+"F5.opPattern","COPY",BODY,{"derivedFrom":makeQuery(id+"F4.opPattern","COPY",BODY,{"derivedFrom":makeQuery(id+"F2.opPattern","COPY",BODY,{"derivedFrom":makeQuery(id+"F1.opRevolve","SWEPT_BODY",BODY,{"disambiguationData":[OSD([sQuery(id+"F0.wireOp",EDGE,"E1")])]}),"instanceName":"1"}),"instanceName":"1"}),"instanceName":"1"}),"instanceName":"1"}),"instanceName":"1"});
            var Q70;
            Q70=makeQuery(id+"F8.opPattern","COPY",BODY,{"derivedFrom":makeQuery(id+"F6.opPattern","COPY",BODY,{"derivedFrom":makeQuery(id+"F5.opPattern","COPY",BODY,{"derivedFrom":makeQuery(id+"F4.opPattern","COPY",BODY,{"derivedFrom":makeQuery(id+"F3.opPattern","COPY",BODY,{"derivedFrom":makeQuery(id+"F2.opPattern","COPY",BODY,{"derivedFrom":makeQuery(id+"F1.opRevolve","SWEPT_BODY",BODY,{"disambiguationData":[OSD([sQuery(id+"F0.wireOp",EDGE,"E1")])]}),"instanceName":"1"}),"instanceName":"1"}),"instanceName":"1"}),"instanceName":"1"}),"instanceName":"1"}),"instanceName":"1"});
            var Q71;
            Q71=makeQuery(id+"F8.opPattern","COPY",BODY,{"derivedFrom":makeQuery(id+"F7.opPattern","COPY",BODY,{"derivedFrom":makeQuery(id+"F1.opRevolve","SWEPT_BODY",BODY,{"disambiguationData":[OSD([sQuery(id+"F0.wireOp",EDGE,"E1")])]}),"instanceName":"1"}),"instanceName":"1"});
            var Q72;
            Q72=makeQuery(id+"F8.opPattern","COPY",BODY,{"derivedFrom":makeQuery(id+"F7.opPattern","COPY",BODY,{"derivedFrom":makeQuery(id+"F2.opPattern","COPY",BODY,{"derivedFrom":makeQuery(id+"F1.opRevolve","SWEPT_BODY",BODY,{"disambiguationData":[OSD([sQuery(id+"F0.wireOp",EDGE,"E1")])]}),"instanceName":"1"}),"instanceName":"1"}),"instanceName":"1"});
            var Q73;
            Q73=makeQuery(id+"F8.opPattern","COPY",BODY,{"derivedFrom":makeQuery(id+"F7.opPattern","COPY",BODY,{"derivedFrom":makeQuery(id+"F3.opPattern","COPY",BODY,{"derivedFrom":makeQuery(id+"F2.opPattern","COPY",BODY,{"derivedFrom":makeQuery(id+"F1.opRevolve","SWEPT_BODY",BODY,{"disambiguationData":[OSD([sQuery(id+"F0.wireOp",EDGE,"E1")])]}),"instanceName":"1"}),"instanceName":"1"}),"instanceName":"1"}),"instanceName":"1"});
            var Q74;
            Q74=makeQuery(id+"F8.opPattern","COPY",BODY,{"derivedFrom":makeQuery(id+"F7.opPattern","COPY",BODY,{"derivedFrom":makeQuery(id+"F4.opPattern","COPY",BODY,{"derivedFrom":makeQuery(id+"F1.opRevolve","SWEPT_BODY",BODY,{"disambiguationData":[OSD([sQuery(id+"F0.wireOp",EDGE,"E1")])]}),"instanceName":"1"}),"instanceName":"1"}),"instanceName":"1"});
            var Q75;
            Q75=makeQuery(id+"F8.opPattern","COPY",BODY,{"derivedFrom":makeQuery(id+"F7.opPattern","COPY",BODY,{"derivedFrom":makeQuery(id+"F4.opPattern","COPY",BODY,{"derivedFrom":makeQuery(id+"F2.opPattern","COPY",BODY,{"derivedFrom":makeQuery(id+"F1.opRevolve","SWEPT_BODY",BODY,{"disambiguationData":[OSD([sQuery(id+"F0.wireOp",EDGE,"E1")])]}),"instanceName":"1"}),"instanceName":"1"}),"instanceName":"1"}),"instanceName":"1"});
            var Q76;
            Q76=makeQuery(id+"F8.opPattern","COPY",BODY,{"derivedFrom":makeQuery(id+"F7.opPattern","COPY",BODY,{"derivedFrom":makeQuery(id+"F4.opPattern","COPY",BODY,{"derivedFrom":makeQuery(id+"F3.opPattern","COPY",BODY,{"derivedFrom":makeQuery(id+"F2.opPattern","COPY",BODY,{"derivedFrom":makeQuery(id+"F1.opRevolve","SWEPT_BODY",BODY,{"disambiguationData":[OSD([sQuery(id+"F0.wireOp",EDGE,"E1")])]}),"instanceName":"1"}),"instanceName":"1"}),"instanceName":"1"}),"instanceName":"1"}),"instanceName":"1"});
            var Q77;
            Q77=makeQuery(id+"F8.opPattern","COPY",BODY,{"derivedFrom":makeQuery(id+"F7.opPattern","COPY",BODY,{"derivedFrom":makeQuery(id+"F5.opPattern","COPY",BODY,{"derivedFrom":makeQuery(id+"F1.opRevolve","SWEPT_BODY",BODY,{"disambiguationData":[OSD([sQuery(id+"F0.wireOp",EDGE,"E1")])]}),"instanceName":"1"}),"instanceName":"1"}),"instanceName":"1"});
            var Q78;
            Q78=makeQuery(id+"F8.opPattern","COPY",BODY,{"derivedFrom":makeQuery(id+"F7.opPattern","COPY",BODY,{"derivedFrom":makeQuery(id+"F5.opPattern","COPY",BODY,{"derivedFrom":makeQuery(id+"F2.opPattern","COPY",BODY,{"derivedFrom":makeQuery(id+"F1.opRevolve","SWEPT_BODY",BODY,{"disambiguationData":[OSD([sQuery(id+"F0.wireOp",EDGE,"E1")])]}),"instanceName":"1"}),"instanceName":"1"}),"instanceName":"1"}),"instanceName":"1"});
            var Q79;
            Q79=makeQuery(id+"F8.opPattern","COPY",BODY,{"derivedFrom":makeQuery(id+"F7.opPattern","COPY",BODY,{"derivedFrom":makeQuery(id+"F5.opPattern","COPY",BODY,{"derivedFrom":makeQuery(id+"F3.opPattern","COPY",BODY,{"derivedFrom":makeQuery(id+"F2.opPattern","COPY",BODY,{"derivedFrom":makeQuery(id+"F1.opRevolve","SWEPT_BODY",BODY,{"disambiguationData":[OSD([sQuery(id+"F0.wireOp",EDGE,"E1")])]}),"instanceName":"1"}),"instanceName":"1"}),"instanceName":"1"}),"instanceName":"1"}),"instanceName":"1"});
            var Q80;
            Q80=makeQuery(id+"F8.opPattern","COPY",BODY,{"derivedFrom":makeQuery(id+"F7.opPattern","COPY",BODY,{"derivedFrom":makeQuery(id+"F5.opPattern","COPY",BODY,{"derivedFrom":makeQuery(id+"F4.opPattern","COPY",BODY,{"derivedFrom":makeQuery(id+"F1.opRevolve","SWEPT_BODY",BODY,{"disambiguationData":[OSD([sQuery(id+"F0.wireOp",EDGE,"E1")])]}),"instanceName":"1"}),"instanceName":"1"}),"instanceName":"1"}),"instanceName":"1"});
            var Q81;
            Q81=makeQuery(id+"F8.opPattern","COPY",BODY,{"derivedFrom":makeQuery(id+"F7.opPattern","COPY",BODY,{"derivedFrom":makeQuery(id+"F5.opPattern","COPY",BODY,{"derivedFrom":makeQuery(id+"F4.opPattern","COPY",BODY,{"derivedFrom":makeQuery(id+"F2.opPattern","COPY",BODY,{"derivedFrom":makeQuery(id+"F1.opRevolve","SWEPT_BODY",BODY,{"disambiguationData":[OSD([sQuery(id+"F0.wireOp",EDGE,"E1")])]}),"instanceName":"1"}),"instanceName":"1"}),"instanceName":"1"}),"instanceName":"1"}),"instanceName":"1"});
            var Q82;
            Q82=makeQuery(id+"F8.opPattern","COPY",BODY,{"derivedFrom":makeQuery(id+"F7.opPattern","COPY",BODY,{"derivedFrom":makeQuery(id+"F5.opPattern","COPY",BODY,{"derivedFrom":makeQuery(id+"F4.opPattern","COPY",BODY,{"derivedFrom":makeQuery(id+"F3.opPattern","COPY",BODY,{"derivedFrom":makeQuery(id+"F2.opPattern","COPY",BODY,{"derivedFrom":makeQuery(id+"F1.opRevolve","SWEPT_BODY",BODY,{"disambiguationData":[OSD([sQuery(id+"F0.wireOp",EDGE,"E1")])]}),"instanceName":"1"}),"instanceName":"1"}),"instanceName":"1"}),"instanceName":"1"}),"instanceName":"1"}),"instanceName":"1"});
            var Q83;
            Q83=makeQuery(id+"F8.opPattern","COPY",BODY,{"derivedFrom":makeQuery(id+"F7.opPattern","COPY",BODY,{"derivedFrom":makeQuery(id+"F6.opPattern","COPY",BODY,{"derivedFrom":makeQuery(id+"F1.opRevolve","SWEPT_BODY",BODY,{"disambiguationData":[OSD([sQuery(id+"F0.wireOp",EDGE,"E1")])]}),"instanceName":"1"}),"instanceName":"1"}),"instanceName":"1"});
            var Q84;
            Q84=makeQuery(id+"F8.opPattern","COPY",BODY,{"derivedFrom":makeQuery(id+"F7.opPattern","COPY",BODY,{"derivedFrom":makeQuery(id+"F6.opPattern","COPY",BODY,{"derivedFrom":makeQuery(id+"F2.opPattern","COPY",BODY,{"derivedFrom":makeQuery(id+"F1.opRevolve","SWEPT_BODY",BODY,{"disambiguationData":[OSD([sQuery(id+"F0.wireOp",EDGE,"E1")])]}),"instanceName":"1"}),"instanceName":"1"}),"instanceName":"1"}),"instanceName":"1"});
            var Q85;
            Q85=makeQuery(id+"F8.opPattern","COPY",BODY,{"derivedFrom":makeQuery(id+"F7.opPattern","COPY",BODY,{"derivedFrom":makeQuery(id+"F6.opPattern","COPY",BODY,{"derivedFrom":makeQuery(id+"F3.opPattern","COPY",BODY,{"derivedFrom":makeQuery(id+"F2.opPattern","COPY",BODY,{"derivedFrom":makeQuery(id+"F1.opRevolve","SWEPT_BODY",BODY,{"disambiguationData":[OSD([sQuery(id+"F0.wireOp",EDGE,"E1")])]}),"instanceName":"1"}),"instanceName":"1"}),"instanceName":"1"}),"instanceName":"1"}),"instanceName":"1"});
            var Q86;
            Q86=makeQuery(id+"F8.opPattern","COPY",BODY,{"derivedFrom":makeQuery(id+"F7.opPattern","COPY",BODY,{"derivedFrom":makeQuery(id+"F6.opPattern","COPY",BODY,{"derivedFrom":makeQuery(id+"F4.opPattern","COPY",BODY,{"derivedFrom":makeQuery(id+"F1.opRevolve","SWEPT_BODY",BODY,{"disambiguationData":[OSD([sQuery(id+"F0.wireOp",EDGE,"E1")])]}),"instanceName":"1"}),"instanceName":"1"}),"instanceName":"1"}),"instanceName":"1"});
            var Q87;
            Q87=makeQuery(id+"F8.opPattern","COPY",BODY,{"derivedFrom":makeQuery(id+"F7.opPattern","COPY",BODY,{"derivedFrom":makeQuery(id+"F6.opPattern","COPY",BODY,{"derivedFrom":makeQuery(id+"F4.opPattern","COPY",BODY,{"derivedFrom":makeQuery(id+"F2.opPattern","COPY",BODY,{"derivedFrom":makeQuery(id+"F1.opRevolve","SWEPT_BODY",BODY,{"disambiguationData":[OSD([sQuery(id+"F0.wireOp",EDGE,"E1")])]}),"instanceName":"1"}),"instanceName":"1"}),"instanceName":"1"}),"instanceName":"1"}),"instanceName":"1"});
            var Q88;
            Q88=makeQuery(id+"F8.opPattern","COPY",BODY,{"derivedFrom":makeQuery(id+"F7.opPattern","COPY",BODY,{"derivedFrom":makeQuery(id+"F6.opPattern","COPY",BODY,{"derivedFrom":makeQuery(id+"F4.opPattern","COPY",BODY,{"derivedFrom":makeQuery(id+"F3.opPattern","COPY",BODY,{"derivedFrom":makeQuery(id+"F2.opPattern","COPY",BODY,{"derivedFrom":makeQuery(id+"F1.opRevolve","SWEPT_BODY",BODY,{"disambiguationData":[OSD([sQuery(id+"F0.wireOp",EDGE,"E1")])]}),"instanceName":"1"}),"instanceName":"1"}),"instanceName":"1"}),"instanceName":"1"}),"instanceName":"1"}),"instanceName":"1"});
            var Q89;
            Q89=makeQuery(id+"F8.opPattern","COPY",BODY,{"derivedFrom":makeQuery(id+"F7.opPattern","COPY",BODY,{"derivedFrom":makeQuery(id+"F6.opPattern","COPY",BODY,{"derivedFrom":makeQuery(id+"F5.opPattern","COPY",BODY,{"derivedFrom":makeQuery(id+"F1.opRevolve","SWEPT_BODY",BODY,{"disambiguationData":[OSD([sQuery(id+"F0.wireOp",EDGE,"E1")])]}),"instanceName":"1"}),"instanceName":"1"}),"instanceName":"1"}),"instanceName":"1"});
            var Q90;
            Q90=makeQuery(id+"F8.opPattern","COPY",BODY,{"derivedFrom":makeQuery(id+"F7.opPattern","COPY",BODY,{"derivedFrom":makeQuery(id+"F6.opPattern","COPY",BODY,{"derivedFrom":makeQuery(id+"F5.opPattern","COPY",BODY,{"derivedFrom":makeQuery(id+"F2.opPattern","COPY",BODY,{"derivedFrom":makeQuery(id+"F1.opRevolve","SWEPT_BODY",BODY,{"disambiguationData":[OSD([sQuery(id+"F0.wireOp",EDGE,"E1")])]}),"instanceName":"1"}),"instanceName":"1"}),"instanceName":"1"}),"instanceName":"1"}),"instanceName":"1"});
            var Q91;
            Q91=makeQuery(id+"F8.opPattern","COPY",BODY,{"derivedFrom":makeQuery(id+"F7.opPattern","COPY",BODY,{"derivedFrom":makeQuery(id+"F6.opPattern","COPY",BODY,{"derivedFrom":makeQuery(id+"F5.opPattern","COPY",BODY,{"derivedFrom":makeQuery(id+"F3.opPattern","COPY",BODY,{"derivedFrom":makeQuery(id+"F2.opPattern","COPY",BODY,{"derivedFrom":makeQuery(id+"F1.opRevolve","SWEPT_BODY",BODY,{"disambiguationData":[OSD([sQuery(id+"F0.wireOp",EDGE,"E1")])]}),"instanceName":"1"}),"instanceName":"1"}),"instanceName":"1"}),"instanceName":"1"}),"instanceName":"1"}),"instanceName":"1"});
            var Q92;
            Q92=makeQuery(id+"F8.opPattern","COPY",BODY,{"derivedFrom":makeQuery(id+"F7.opPattern","COPY",BODY,{"derivedFrom":makeQuery(id+"F6.opPattern","COPY",BODY,{"derivedFrom":makeQuery(id+"F5.opPattern","COPY",BODY,{"derivedFrom":makeQuery(id+"F4.opPattern","COPY",BODY,{"derivedFrom":makeQuery(id+"F1.opRevolve","SWEPT_BODY",BODY,{"disambiguationData":[OSD([sQuery(id+"F0.wireOp",EDGE,"E1")])]}),"instanceName":"1"}),"instanceName":"1"}),"instanceName":"1"}),"instanceName":"1"}),"instanceName":"1"});
            var Q93;
            Q93=makeQuery(id+"F8.opPattern","COPY",BODY,{"derivedFrom":makeQuery(id+"F7.opPattern","COPY",BODY,{"derivedFrom":makeQuery(id+"F6.opPattern","COPY",BODY,{"derivedFrom":makeQuery(id+"F5.opPattern","COPY",BODY,{"derivedFrom":makeQuery(id+"F4.opPattern","COPY",BODY,{"derivedFrom":makeQuery(id+"F2.opPattern","COPY",BODY,{"derivedFrom":makeQuery(id+"F1.opRevolve","SWEPT_BODY",BODY,{"disambiguationData":[OSD([sQuery(id+"F0.wireOp",EDGE,"E1")])]}),"instanceName":"1"}),"instanceName":"1"}),"instanceName":"1"}),"instanceName":"1"}),"instanceName":"1"}),"instanceName":"1"});
            var Q94;
            Q94=makeQuery(id+"F8.opPattern","COPY",BODY,{"derivedFrom":makeQuery(id+"F7.opPattern","COPY",BODY,{"derivedFrom":makeQuery(id+"F6.opPattern","COPY",BODY,{"derivedFrom":makeQuery(id+"F5.opPattern","COPY",BODY,{"derivedFrom":makeQuery(id+"F4.opPattern","COPY",BODY,{"derivedFrom":makeQuery(id+"F3.opPattern","COPY",BODY,{"derivedFrom":makeQuery(id+"F2.opPattern","COPY",BODY,{"derivedFrom":makeQuery(id+"F1.opRevolve","SWEPT_BODY",BODY,{"disambiguationData":[OSD([sQuery(id+"F0.wireOp",EDGE,"E1")])]}),"instanceName":"1"}),"instanceName":"1"}),"instanceName":"1"}),"instanceName":"1"}),"instanceName":"1"}),"instanceName":"1"}),"instanceName":"1"});
            var Q95;
            Q95=makeQuery(id+"F9.opPattern","COPY",BODY,{"derivedFrom":makeQuery(id+"F1.opRevolve","SWEPT_BODY",BODY,{"disambiguationData":[OSD([sQuery(id+"F0.wireOp",EDGE,"E1")])]}),"instanceName":"1"});
            var Q96;
            Q96=makeQuery(id+"F9.opPattern","COPY",BODY,{"derivedFrom":makeQuery(id+"F2.opPattern","COPY",BODY,{"derivedFrom":makeQuery(id+"F1.opRevolve","SWEPT_BODY",BODY,{"disambiguationData":[OSD([sQuery(id+"F0.wireOp",EDGE,"E1")])]}),"instanceName":"1"}),"instanceName":"1"});
            var Q97;
            Q97=makeQuery(id+"F9.opPattern","COPY",BODY,{"derivedFrom":makeQuery(id+"F3.opPattern","COPY",BODY,{"derivedFrom":makeQuery(id+"F2.opPattern","COPY",BODY,{"derivedFrom":makeQuery(id+"F1.opRevolve","SWEPT_BODY",BODY,{"disambiguationData":[OSD([sQuery(id+"F0.wireOp",EDGE,"E1")])]}),"instanceName":"1"}),"instanceName":"1"}),"instanceName":"1"});
            var Q98;
            Q98=makeQuery(id+"F9.opPattern","COPY",BODY,{"derivedFrom":makeQuery(id+"F4.opPattern","COPY",BODY,{"derivedFrom":makeQuery(id+"F1.opRevolve","SWEPT_BODY",BODY,{"disambiguationData":[OSD([sQuery(id+"F0.wireOp",EDGE,"E1")])]}),"instanceName":"1"}),"instanceName":"1"});
            var Q99;
            Q99=makeQuery(id+"F9.opPattern","COPY",BODY,{"derivedFrom":makeQuery(id+"F4.opPattern","COPY",BODY,{"derivedFrom":makeQuery(id+"F2.opPattern","COPY",BODY,{"derivedFrom":makeQuery(id+"F1.opRevolve","SWEPT_BODY",BODY,{"disambiguationData":[OSD([sQuery(id+"F0.wireOp",EDGE,"E1")])]}),"instanceName":"1"}),"instanceName":"1"}),"instanceName":"1"});
            var Q100;
            Q100=makeQuery(id+"F9.opPattern","COPY",BODY,{"derivedFrom":makeQuery(id+"F4.opPattern","COPY",BODY,{"derivedFrom":makeQuery(id+"F3.opPattern","COPY",BODY,{"derivedFrom":makeQuery(id+"F2.opPattern","COPY",BODY,{"derivedFrom":makeQuery(id+"F1.opRevolve","SWEPT_BODY",BODY,{"disambiguationData":[OSD([sQuery(id+"F0.wireOp",EDGE,"E1")])]}),"instanceName":"1"}),"instanceName":"1"}),"instanceName":"1"}),"instanceName":"1"});
            var Q101;
            Q101=makeQuery(id+"F9.opPattern","COPY",BODY,{"derivedFrom":makeQuery(id+"F5.opPattern","COPY",BODY,{"derivedFrom":makeQuery(id+"F1.opRevolve","SWEPT_BODY",BODY,{"disambiguationData":[OSD([sQuery(id+"F0.wireOp",EDGE,"E1")])]}),"instanceName":"1"}),"instanceName":"1"});
            var Q102;
            Q102=makeQuery(id+"F9.opPattern","COPY",BODY,{"derivedFrom":makeQuery(id+"F5.opPattern","COPY",BODY,{"derivedFrom":makeQuery(id+"F2.opPattern","COPY",BODY,{"derivedFrom":makeQuery(id+"F1.opRevolve","SWEPT_BODY",BODY,{"disambiguationData":[OSD([sQuery(id+"F0.wireOp",EDGE,"E1")])]}),"instanceName":"1"}),"instanceName":"1"}),"instanceName":"1"});
            var Q103;
            Q103=makeQuery(id+"F9.opPattern","COPY",BODY,{"derivedFrom":makeQuery(id+"F5.opPattern","COPY",BODY,{"derivedFrom":makeQuery(id+"F3.opPattern","COPY",BODY,{"derivedFrom":makeQuery(id+"F2.opPattern","COPY",BODY,{"derivedFrom":makeQuery(id+"F1.opRevolve","SWEPT_BODY",BODY,{"disambiguationData":[OSD([sQuery(id+"F0.wireOp",EDGE,"E1")])]}),"instanceName":"1"}),"instanceName":"1"}),"instanceName":"1"}),"instanceName":"1"});
            var Q104;
            Q104=makeQuery(id+"F9.opPattern","COPY",BODY,{"derivedFrom":makeQuery(id+"F5.opPattern","COPY",BODY,{"derivedFrom":makeQuery(id+"F4.opPattern","COPY",BODY,{"derivedFrom":makeQuery(id+"F1.opRevolve","SWEPT_BODY",BODY,{"disambiguationData":[OSD([sQuery(id+"F0.wireOp",EDGE,"E1")])]}),"instanceName":"1"}),"instanceName":"1"}),"instanceName":"1"});
            var Q105;
            Q105=makeQuery(id+"F9.opPattern","COPY",BODY,{"derivedFrom":makeQuery(id+"F5.opPattern","COPY",BODY,{"derivedFrom":makeQuery(id+"F4.opPattern","COPY",BODY,{"derivedFrom":makeQuery(id+"F2.opPattern","COPY",BODY,{"derivedFrom":makeQuery(id+"F1.opRevolve","SWEPT_BODY",BODY,{"disambiguationData":[OSD([sQuery(id+"F0.wireOp",EDGE,"E1")])]}),"instanceName":"1"}),"instanceName":"1"}),"instanceName":"1"}),"instanceName":"1"});
            var Q106;
            Q106=makeQuery(id+"F9.opPattern","COPY",BODY,{"derivedFrom":makeQuery(id+"F5.opPattern","COPY",BODY,{"derivedFrom":makeQuery(id+"F4.opPattern","COPY",BODY,{"derivedFrom":makeQuery(id+"F3.opPattern","COPY",BODY,{"derivedFrom":makeQuery(id+"F2.opPattern","COPY",BODY,{"derivedFrom":makeQuery(id+"F1.opRevolve","SWEPT_BODY",BODY,{"disambiguationData":[OSD([sQuery(id+"F0.wireOp",EDGE,"E1")])]}),"instanceName":"1"}),"instanceName":"1"}),"instanceName":"1"}),"instanceName":"1"}),"instanceName":"1"});
            var Q107;
            Q107=makeQuery(id+"F9.opPattern","COPY",BODY,{"derivedFrom":makeQuery(id+"F6.opPattern","COPY",BODY,{"derivedFrom":makeQuery(id+"F1.opRevolve","SWEPT_BODY",BODY,{"disambiguationData":[OSD([sQuery(id+"F0.wireOp",EDGE,"E1")])]}),"instanceName":"1"}),"instanceName":"1"});
            var Q108;
            Q108=makeQuery(id+"F9.opPattern","COPY",BODY,{"derivedFrom":makeQuery(id+"F6.opPattern","COPY",BODY,{"derivedFrom":makeQuery(id+"F2.opPattern","COPY",BODY,{"derivedFrom":makeQuery(id+"F1.opRevolve","SWEPT_BODY",BODY,{"disambiguationData":[OSD([sQuery(id+"F0.wireOp",EDGE,"E1")])]}),"instanceName":"1"}),"instanceName":"1"}),"instanceName":"1"});
            var Q109;
            Q109=makeQuery(id+"F9.opPattern","COPY",BODY,{"derivedFrom":makeQuery(id+"F6.opPattern","COPY",BODY,{"derivedFrom":makeQuery(id+"F3.opPattern","COPY",BODY,{"derivedFrom":makeQuery(id+"F2.opPattern","COPY",BODY,{"derivedFrom":makeQuery(id+"F1.opRevolve","SWEPT_BODY",BODY,{"disambiguationData":[OSD([sQuery(id+"F0.wireOp",EDGE,"E1")])]}),"instanceName":"1"}),"instanceName":"1"}),"instanceName":"1"}),"instanceName":"1"});
            var Q110;
            Q110=makeQuery(id+"F9.opPattern","COPY",BODY,{"derivedFrom":makeQuery(id+"F6.opPattern","COPY",BODY,{"derivedFrom":makeQuery(id+"F4.opPattern","COPY",BODY,{"derivedFrom":makeQuery(id+"F1.opRevolve","SWEPT_BODY",BODY,{"disambiguationData":[OSD([sQuery(id+"F0.wireOp",EDGE,"E1")])]}),"instanceName":"1"}),"instanceName":"1"}),"instanceName":"1"});
            var Q111;
            Q111=makeQuery(id+"F9.opPattern","COPY",BODY,{"derivedFrom":makeQuery(id+"F6.opPattern","COPY",BODY,{"derivedFrom":makeQuery(id+"F4.opPattern","COPY",BODY,{"derivedFrom":makeQuery(id+"F2.opPattern","COPY",BODY,{"derivedFrom":makeQuery(id+"F1.opRevolve","SWEPT_BODY",BODY,{"disambiguationData":[OSD([sQuery(id+"F0.wireOp",EDGE,"E1")])]}),"instanceName":"1"}),"instanceName":"1"}),"instanceName":"1"}),"instanceName":"1"});
            var Q112;
            Q112=makeQuery(id+"F9.opPattern","COPY",BODY,{"derivedFrom":makeQuery(id+"F6.opPattern","COPY",BODY,{"derivedFrom":makeQuery(id+"F4.opPattern","COPY",BODY,{"derivedFrom":makeQuery(id+"F3.opPattern","COPY",BODY,{"derivedFrom":makeQuery(id+"F2.opPattern","COPY",BODY,{"derivedFrom":makeQuery(id+"F1.opRevolve","SWEPT_BODY",BODY,{"disambiguationData":[OSD([sQuery(id+"F0.wireOp",EDGE,"E1")])]}),"instanceName":"1"}),"instanceName":"1"}),"instanceName":"1"}),"instanceName":"1"}),"instanceName":"1"});
            var Q113;
            Q113=makeQuery(id+"F9.opPattern","COPY",BODY,{"derivedFrom":makeQuery(id+"F6.opPattern","COPY",BODY,{"derivedFrom":makeQuery(id+"F5.opPattern","COPY",BODY,{"derivedFrom":makeQuery(id+"F1.opRevolve","SWEPT_BODY",BODY,{"disambiguationData":[OSD([sQuery(id+"F0.wireOp",EDGE,"E1")])]}),"instanceName":"1"}),"instanceName":"1"}),"instanceName":"1"});
            var Q114;
            Q114=makeQuery(id+"F9.opPattern","COPY",BODY,{"derivedFrom":makeQuery(id+"F6.opPattern","COPY",BODY,{"derivedFrom":makeQuery(id+"F5.opPattern","COPY",BODY,{"derivedFrom":makeQuery(id+"F2.opPattern","COPY",BODY,{"derivedFrom":makeQuery(id+"F1.opRevolve","SWEPT_BODY",BODY,{"disambiguationData":[OSD([sQuery(id+"F0.wireOp",EDGE,"E1")])]}),"instanceName":"1"}),"instanceName":"1"}),"instanceName":"1"}),"instanceName":"1"});
            var Q115;
            Q115=makeQuery(id+"F9.opPattern","COPY",BODY,{"derivedFrom":makeQuery(id+"F6.opPattern","COPY",BODY,{"derivedFrom":makeQuery(id+"F5.opPattern","COPY",BODY,{"derivedFrom":makeQuery(id+"F3.opPattern","COPY",BODY,{"derivedFrom":makeQuery(id+"F2.opPattern","COPY",BODY,{"derivedFrom":makeQuery(id+"F1.opRevolve","SWEPT_BODY",BODY,{"disambiguationData":[OSD([sQuery(id+"F0.wireOp",EDGE,"E1")])]}),"instanceName":"1"}),"instanceName":"1"}),"instanceName":"1"}),"instanceName":"1"}),"instanceName":"1"});
            var Q116;
            Q116=makeQuery(id+"F9.opPattern","COPY",BODY,{"derivedFrom":makeQuery(id+"F6.opPattern","COPY",BODY,{"derivedFrom":makeQuery(id+"F5.opPattern","COPY",BODY,{"derivedFrom":makeQuery(id+"F4.opPattern","COPY",BODY,{"derivedFrom":makeQuery(id+"F1.opRevolve","SWEPT_BODY",BODY,{"disambiguationData":[OSD([sQuery(id+"F0.wireOp",EDGE,"E1")])]}),"instanceName":"1"}),"instanceName":"1"}),"instanceName":"1"}),"instanceName":"1"});
            var Q117;
            Q117=makeQuery(id+"F9.opPattern","COPY",BODY,{"derivedFrom":makeQuery(id+"F6.opPattern","COPY",BODY,{"derivedFrom":makeQuery(id+"F5.opPattern","COPY",BODY,{"derivedFrom":makeQuery(id+"F4.opPattern","COPY",BODY,{"derivedFrom":makeQuery(id+"F2.opPattern","COPY",BODY,{"derivedFrom":makeQuery(id+"F1.opRevolve","SWEPT_BODY",BODY,{"disambiguationData":[OSD([sQuery(id+"F0.wireOp",EDGE,"E1")])]}),"instanceName":"1"}),"instanceName":"1"}),"instanceName":"1"}),"instanceName":"1"}),"instanceName":"1"});
            var Q118;
            Q118=makeQuery(id+"F9.opPattern","COPY",BODY,{"derivedFrom":makeQuery(id+"F6.opPattern","COPY",BODY,{"derivedFrom":makeQuery(id+"F5.opPattern","COPY",BODY,{"derivedFrom":makeQuery(id+"F4.opPattern","COPY",BODY,{"derivedFrom":makeQuery(id+"F3.opPattern","COPY",BODY,{"derivedFrom":makeQuery(id+"F2.opPattern","COPY",BODY,{"derivedFrom":makeQuery(id+"F1.opRevolve","SWEPT_BODY",BODY,{"disambiguationData":[OSD([sQuery(id+"F0.wireOp",EDGE,"E1")])]}),"instanceName":"1"}),"instanceName":"1"}),"instanceName":"1"}),"instanceName":"1"}),"instanceName":"1"}),"instanceName":"1"});
            var Q119;
            Q119=makeQuery(id+"F9.opPattern","COPY",BODY,{"derivedFrom":makeQuery(id+"F7.opPattern","COPY",BODY,{"derivedFrom":makeQuery(id+"F1.opRevolve","SWEPT_BODY",BODY,{"disambiguationData":[OSD([sQuery(id+"F0.wireOp",EDGE,"E1")])]}),"instanceName":"1"}),"instanceName":"1"});
            var Q120;
            Q120=makeQuery(id+"F9.opPattern","COPY",BODY,{"derivedFrom":makeQuery(id+"F7.opPattern","COPY",BODY,{"derivedFrom":makeQuery(id+"F2.opPattern","COPY",BODY,{"derivedFrom":makeQuery(id+"F1.opRevolve","SWEPT_BODY",BODY,{"disambiguationData":[OSD([sQuery(id+"F0.wireOp",EDGE,"E1")])]}),"instanceName":"1"}),"instanceName":"1"}),"instanceName":"1"});
            var Q121;
            Q121=makeQuery(id+"F9.opPattern","COPY",BODY,{"derivedFrom":makeQuery(id+"F7.opPattern","COPY",BODY,{"derivedFrom":makeQuery(id+"F3.opPattern","COPY",BODY,{"derivedFrom":makeQuery(id+"F2.opPattern","COPY",BODY,{"derivedFrom":makeQuery(id+"F1.opRevolve","SWEPT_BODY",BODY,{"disambiguationData":[OSD([sQuery(id+"F0.wireOp",EDGE,"E1")])]}),"instanceName":"1"}),"instanceName":"1"}),"instanceName":"1"}),"instanceName":"1"});
            var Q122;
            Q122=makeQuery(id+"F9.opPattern","COPY",BODY,{"derivedFrom":makeQuery(id+"F7.opPattern","COPY",BODY,{"derivedFrom":makeQuery(id+"F4.opPattern","COPY",BODY,{"derivedFrom":makeQuery(id+"F1.opRevolve","SWEPT_BODY",BODY,{"disambiguationData":[OSD([sQuery(id+"F0.wireOp",EDGE,"E1")])]}),"instanceName":"1"}),"instanceName":"1"}),"instanceName":"1"});
            var Q123;
            Q123=makeQuery(id+"F9.opPattern","COPY",BODY,{"derivedFrom":makeQuery(id+"F7.opPattern","COPY",BODY,{"derivedFrom":makeQuery(id+"F4.opPattern","COPY",BODY,{"derivedFrom":makeQuery(id+"F2.opPattern","COPY",BODY,{"derivedFrom":makeQuery(id+"F1.opRevolve","SWEPT_BODY",BODY,{"disambiguationData":[OSD([sQuery(id+"F0.wireOp",EDGE,"E1")])]}),"instanceName":"1"}),"instanceName":"1"}),"instanceName":"1"}),"instanceName":"1"});
            var Q124;
            Q124=makeQuery(id+"F9.opPattern","COPY",BODY,{"derivedFrom":makeQuery(id+"F7.opPattern","COPY",BODY,{"derivedFrom":makeQuery(id+"F4.opPattern","COPY",BODY,{"derivedFrom":makeQuery(id+"F3.opPattern","COPY",BODY,{"derivedFrom":makeQuery(id+"F2.opPattern","COPY",BODY,{"derivedFrom":makeQuery(id+"F1.opRevolve","SWEPT_BODY",BODY,{"disambiguationData":[OSD([sQuery(id+"F0.wireOp",EDGE,"E1")])]}),"instanceName":"1"}),"instanceName":"1"}),"instanceName":"1"}),"instanceName":"1"}),"instanceName":"1"});
            var Q125;
            Q125=makeQuery(id+"F9.opPattern","COPY",BODY,{"derivedFrom":makeQuery(id+"F7.opPattern","COPY",BODY,{"derivedFrom":makeQuery(id+"F5.opPattern","COPY",BODY,{"derivedFrom":makeQuery(id+"F1.opRevolve","SWEPT_BODY",BODY,{"disambiguationData":[OSD([sQuery(id+"F0.wireOp",EDGE,"E1")])]}),"instanceName":"1"}),"instanceName":"1"}),"instanceName":"1"});
            var Q126;
            Q126=makeQuery(id+"F9.opPattern","COPY",BODY,{"derivedFrom":makeQuery(id+"F7.opPattern","COPY",BODY,{"derivedFrom":makeQuery(id+"F5.opPattern","COPY",BODY,{"derivedFrom":makeQuery(id+"F2.opPattern","COPY",BODY,{"derivedFrom":makeQuery(id+"F1.opRevolve","SWEPT_BODY",BODY,{"disambiguationData":[OSD([sQuery(id+"F0.wireOp",EDGE,"E1")])]}),"instanceName":"1"}),"instanceName":"1"}),"instanceName":"1"}),"instanceName":"1"});
            var Q127;
            Q127=makeQuery(id+"F9.opPattern","COPY",BODY,{"derivedFrom":makeQuery(id+"F7.opPattern","COPY",BODY,{"derivedFrom":makeQuery(id+"F5.opPattern","COPY",BODY,{"derivedFrom":makeQuery(id+"F3.opPattern","COPY",BODY,{"derivedFrom":makeQuery(id+"F2.opPattern","COPY",BODY,{"derivedFrom":makeQuery(id+"F1.opRevolve","SWEPT_BODY",BODY,{"disambiguationData":[OSD([sQuery(id+"F0.wireOp",EDGE,"E1")])]}),"instanceName":"1"}),"instanceName":"1"}),"instanceName":"1"}),"instanceName":"1"}),"instanceName":"1"});
            var Q128;
            Q128=makeQuery(id+"F9.opPattern","COPY",BODY,{"derivedFrom":makeQuery(id+"F7.opPattern","COPY",BODY,{"derivedFrom":makeQuery(id+"F5.opPattern","COPY",BODY,{"derivedFrom":makeQuery(id+"F4.opPattern","COPY",BODY,{"derivedFrom":makeQuery(id+"F1.opRevolve","SWEPT_BODY",BODY,{"disambiguationData":[OSD([sQuery(id+"F0.wireOp",EDGE,"E1")])]}),"instanceName":"1"}),"instanceName":"1"}),"instanceName":"1"}),"instanceName":"1"});
            var Q129;
            Q129=makeQuery(id+"F9.opPattern","COPY",BODY,{"derivedFrom":makeQuery(id+"F7.opPattern","COPY",BODY,{"derivedFrom":makeQuery(id+"F5.opPattern","COPY",BODY,{"derivedFrom":makeQuery(id+"F4.opPattern","COPY",BODY,{"derivedFrom":makeQuery(id+"F2.opPattern","COPY",BODY,{"derivedFrom":makeQuery(id+"F1.opRevolve","SWEPT_BODY",BODY,{"disambiguationData":[OSD([sQuery(id+"F0.wireOp",EDGE,"E1")])]}),"instanceName":"1"}),"instanceName":"1"}),"instanceName":"1"}),"instanceName":"1"}),"instanceName":"1"});
            var Q130;
            Q130=makeQuery(id+"F9.opPattern","COPY",BODY,{"derivedFrom":makeQuery(id+"F7.opPattern","COPY",BODY,{"derivedFrom":makeQuery(id+"F5.opPattern","COPY",BODY,{"derivedFrom":makeQuery(id+"F4.opPattern","COPY",BODY,{"derivedFrom":makeQuery(id+"F3.opPattern","COPY",BODY,{"derivedFrom":makeQuery(id+"F2.opPattern","COPY",BODY,{"derivedFrom":makeQuery(id+"F1.opRevolve","SWEPT_BODY",BODY,{"disambiguationData":[OSD([sQuery(id+"F0.wireOp",EDGE,"E1")])]}),"instanceName":"1"}),"instanceName":"1"}),"instanceName":"1"}),"instanceName":"1"}),"instanceName":"1"}),"instanceName":"1"});
            var Q131;
            Q131=makeQuery(id+"F9.opPattern","COPY",BODY,{"derivedFrom":makeQuery(id+"F7.opPattern","COPY",BODY,{"derivedFrom":makeQuery(id+"F6.opPattern","COPY",BODY,{"derivedFrom":makeQuery(id+"F1.opRevolve","SWEPT_BODY",BODY,{"disambiguationData":[OSD([sQuery(id+"F0.wireOp",EDGE,"E1")])]}),"instanceName":"1"}),"instanceName":"1"}),"instanceName":"1"});
            var Q132;
            Q132=makeQuery(id+"F9.opPattern","COPY",BODY,{"derivedFrom":makeQuery(id+"F7.opPattern","COPY",BODY,{"derivedFrom":makeQuery(id+"F6.opPattern","COPY",BODY,{"derivedFrom":makeQuery(id+"F2.opPattern","COPY",BODY,{"derivedFrom":makeQuery(id+"F1.opRevolve","SWEPT_BODY",BODY,{"disambiguationData":[OSD([sQuery(id+"F0.wireOp",EDGE,"E1")])]}),"instanceName":"1"}),"instanceName":"1"}),"instanceName":"1"}),"instanceName":"1"});
            var Q133;
            Q133=makeQuery(id+"F9.opPattern","COPY",BODY,{"derivedFrom":makeQuery(id+"F7.opPattern","COPY",BODY,{"derivedFrom":makeQuery(id+"F6.opPattern","COPY",BODY,{"derivedFrom":makeQuery(id+"F3.opPattern","COPY",BODY,{"derivedFrom":makeQuery(id+"F2.opPattern","COPY",BODY,{"derivedFrom":makeQuery(id+"F1.opRevolve","SWEPT_BODY",BODY,{"disambiguationData":[OSD([sQuery(id+"F0.wireOp",EDGE,"E1")])]}),"instanceName":"1"}),"instanceName":"1"}),"instanceName":"1"}),"instanceName":"1"}),"instanceName":"1"});
            var Q134;
            Q134=makeQuery(id+"F9.opPattern","COPY",BODY,{"derivedFrom":makeQuery(id+"F7.opPattern","COPY",BODY,{"derivedFrom":makeQuery(id+"F6.opPattern","COPY",BODY,{"derivedFrom":makeQuery(id+"F4.opPattern","COPY",BODY,{"derivedFrom":makeQuery(id+"F1.opRevolve","SWEPT_BODY",BODY,{"disambiguationData":[OSD([sQuery(id+"F0.wireOp",EDGE,"E1")])]}),"instanceName":"1"}),"instanceName":"1"}),"instanceName":"1"}),"instanceName":"1"});
            var Q135;
            Q135=makeQuery(id+"F9.opPattern","COPY",BODY,{"derivedFrom":makeQuery(id+"F7.opPattern","COPY",BODY,{"derivedFrom":makeQuery(id+"F6.opPattern","COPY",BODY,{"derivedFrom":makeQuery(id+"F4.opPattern","COPY",BODY,{"derivedFrom":makeQuery(id+"F2.opPattern","COPY",BODY,{"derivedFrom":makeQuery(id+"F1.opRevolve","SWEPT_BODY",BODY,{"disambiguationData":[OSD([sQuery(id+"F0.wireOp",EDGE,"E1")])]}),"instanceName":"1"}),"instanceName":"1"}),"instanceName":"1"}),"instanceName":"1"}),"instanceName":"1"});
            var Q136;
            Q136=makeQuery(id+"F9.opPattern","COPY",BODY,{"derivedFrom":makeQuery(id+"F7.opPattern","COPY",BODY,{"derivedFrom":makeQuery(id+"F6.opPattern","COPY",BODY,{"derivedFrom":makeQuery(id+"F4.opPattern","COPY",BODY,{"derivedFrom":makeQuery(id+"F3.opPattern","COPY",BODY,{"derivedFrom":makeQuery(id+"F2.opPattern","COPY",BODY,{"derivedFrom":makeQuery(id+"F1.opRevolve","SWEPT_BODY",BODY,{"disambiguationData":[OSD([sQuery(id+"F0.wireOp",EDGE,"E1")])]}),"instanceName":"1"}),"instanceName":"1"}),"instanceName":"1"}),"instanceName":"1"}),"instanceName":"1"}),"instanceName":"1"});
            var Q137;
            Q137=makeQuery(id+"F9.opPattern","COPY",BODY,{"derivedFrom":makeQuery(id+"F7.opPattern","COPY",BODY,{"derivedFrom":makeQuery(id+"F6.opPattern","COPY",BODY,{"derivedFrom":makeQuery(id+"F5.opPattern","COPY",BODY,{"derivedFrom":makeQuery(id+"F1.opRevolve","SWEPT_BODY",BODY,{"disambiguationData":[OSD([sQuery(id+"F0.wireOp",EDGE,"E1")])]}),"instanceName":"1"}),"instanceName":"1"}),"instanceName":"1"}),"instanceName":"1"});
            var Q138;
            Q138=makeQuery(id+"F9.opPattern","COPY",BODY,{"derivedFrom":makeQuery(id+"F7.opPattern","COPY",BODY,{"derivedFrom":makeQuery(id+"F6.opPattern","COPY",BODY,{"derivedFrom":makeQuery(id+"F5.opPattern","COPY",BODY,{"derivedFrom":makeQuery(id+"F2.opPattern","COPY",BODY,{"derivedFrom":makeQuery(id+"F1.opRevolve","SWEPT_BODY",BODY,{"disambiguationData":[OSD([sQuery(id+"F0.wireOp",EDGE,"E1")])]}),"instanceName":"1"}),"instanceName":"1"}),"instanceName":"1"}),"instanceName":"1"}),"instanceName":"1"});
            var Q139;
            Q139=makeQuery(id+"F9.opPattern","COPY",BODY,{"derivedFrom":makeQuery(id+"F7.opPattern","COPY",BODY,{"derivedFrom":makeQuery(id+"F6.opPattern","COPY",BODY,{"derivedFrom":makeQuery(id+"F5.opPattern","COPY",BODY,{"derivedFrom":makeQuery(id+"F3.opPattern","COPY",BODY,{"derivedFrom":makeQuery(id+"F2.opPattern","COPY",BODY,{"derivedFrom":makeQuery(id+"F1.opRevolve","SWEPT_BODY",BODY,{"disambiguationData":[OSD([sQuery(id+"F0.wireOp",EDGE,"E1")])]}),"instanceName":"1"}),"instanceName":"1"}),"instanceName":"1"}),"instanceName":"1"}),"instanceName":"1"}),"instanceName":"1"});
            var Q140;
            Q140=makeQuery(id+"F9.opPattern","COPY",BODY,{"derivedFrom":makeQuery(id+"F7.opPattern","COPY",BODY,{"derivedFrom":makeQuery(id+"F6.opPattern","COPY",BODY,{"derivedFrom":makeQuery(id+"F5.opPattern","COPY",BODY,{"derivedFrom":makeQuery(id+"F4.opPattern","COPY",BODY,{"derivedFrom":makeQuery(id+"F1.opRevolve","SWEPT_BODY",BODY,{"disambiguationData":[OSD([sQuery(id+"F0.wireOp",EDGE,"E1")])]}),"instanceName":"1"}),"instanceName":"1"}),"instanceName":"1"}),"instanceName":"1"}),"instanceName":"1"});
            var Q141;
            Q141=makeQuery(id+"F9.opPattern","COPY",BODY,{"derivedFrom":makeQuery(id+"F7.opPattern","COPY",BODY,{"derivedFrom":makeQuery(id+"F6.opPattern","COPY",BODY,{"derivedFrom":makeQuery(id+"F5.opPattern","COPY",BODY,{"derivedFrom":makeQuery(id+"F4.opPattern","COPY",BODY,{"derivedFrom":makeQuery(id+"F2.opPattern","COPY",BODY,{"derivedFrom":makeQuery(id+"F1.opRevolve","SWEPT_BODY",BODY,{"disambiguationData":[OSD([sQuery(id+"F0.wireOp",EDGE,"E1")])]}),"instanceName":"1"}),"instanceName":"1"}),"instanceName":"1"}),"instanceName":"1"}),"instanceName":"1"}),"instanceName":"1"});
            var Q142;
            Q142=makeQuery(id+"F9.opPattern","COPY",BODY,{"derivedFrom":makeQuery(id+"F7.opPattern","COPY",BODY,{"derivedFrom":makeQuery(id+"F6.opPattern","COPY",BODY,{"derivedFrom":makeQuery(id+"F5.opPattern","COPY",BODY,{"derivedFrom":makeQuery(id+"F4.opPattern","COPY",BODY,{"derivedFrom":makeQuery(id+"F3.opPattern","COPY",BODY,{"derivedFrom":makeQuery(id+"F2.opPattern","COPY",BODY,{"derivedFrom":makeQuery(id+"F1.opRevolve","SWEPT_BODY",BODY,{"disambiguationData":[OSD([sQuery(id+"F0.wireOp",EDGE,"E1")])]}),"instanceName":"1"}),"instanceName":"1"}),"instanceName":"1"}),"instanceName":"1"}),"instanceName":"1"}),"instanceName":"1"}),"instanceName":"1"});
            var Q143;
            Q143=makeQuery(id+"F9.opPattern","COPY",BODY,{"derivedFrom":makeQuery(id+"F8.opPattern","COPY",BODY,{"derivedFrom":makeQuery(id+"F1.opRevolve","SWEPT_BODY",BODY,{"disambiguationData":[OSD([sQuery(id+"F0.wireOp",EDGE,"E1")])]}),"instanceName":"1"}),"instanceName":"1"});
            var Q144;
            Q144=makeQuery(id+"F9.opPattern","COPY",BODY,{"derivedFrom":makeQuery(id+"F8.opPattern","COPY",BODY,{"derivedFrom":makeQuery(id+"F2.opPattern","COPY",BODY,{"derivedFrom":makeQuery(id+"F1.opRevolve","SWEPT_BODY",BODY,{"disambiguationData":[OSD([sQuery(id+"F0.wireOp",EDGE,"E1")])]}),"instanceName":"1"}),"instanceName":"1"}),"instanceName":"1"});
            var Q145;
            Q145=makeQuery(id+"F9.opPattern","COPY",BODY,{"derivedFrom":makeQuery(id+"F8.opPattern","COPY",BODY,{"derivedFrom":makeQuery(id+"F3.opPattern","COPY",BODY,{"derivedFrom":makeQuery(id+"F2.opPattern","COPY",BODY,{"derivedFrom":makeQuery(id+"F1.opRevolve","SWEPT_BODY",BODY,{"disambiguationData":[OSD([sQuery(id+"F0.wireOp",EDGE,"E1")])]}),"instanceName":"1"}),"instanceName":"1"}),"instanceName":"1"}),"instanceName":"1"});
            var Q146;
            Q146=makeQuery(id+"F9.opPattern","COPY",BODY,{"derivedFrom":makeQuery(id+"F8.opPattern","COPY",BODY,{"derivedFrom":makeQuery(id+"F4.opPattern","COPY",BODY,{"derivedFrom":makeQuery(id+"F1.opRevolve","SWEPT_BODY",BODY,{"disambiguationData":[OSD([sQuery(id+"F0.wireOp",EDGE,"E1")])]}),"instanceName":"1"}),"instanceName":"1"}),"instanceName":"1"});
            var Q147;
            Q147=makeQuery(id+"F9.opPattern","COPY",BODY,{"derivedFrom":makeQuery(id+"F8.opPattern","COPY",BODY,{"derivedFrom":makeQuery(id+"F4.opPattern","COPY",BODY,{"derivedFrom":makeQuery(id+"F2.opPattern","COPY",BODY,{"derivedFrom":makeQuery(id+"F1.opRevolve","SWEPT_BODY",BODY,{"disambiguationData":[OSD([sQuery(id+"F0.wireOp",EDGE,"E1")])]}),"instanceName":"1"}),"instanceName":"1"}),"instanceName":"1"}),"instanceName":"1"});
            var Q148;
            Q148=makeQuery(id+"F9.opPattern","COPY",BODY,{"derivedFrom":makeQuery(id+"F8.opPattern","COPY",BODY,{"derivedFrom":makeQuery(id+"F4.opPattern","COPY",BODY,{"derivedFrom":makeQuery(id+"F3.opPattern","COPY",BODY,{"derivedFrom":makeQuery(id+"F2.opPattern","COPY",BODY,{"derivedFrom":makeQuery(id+"F1.opRevolve","SWEPT_BODY",BODY,{"disambiguationData":[OSD([sQuery(id+"F0.wireOp",EDGE,"E1")])]}),"instanceName":"1"}),"instanceName":"1"}),"instanceName":"1"}),"instanceName":"1"}),"instanceName":"1"});
            var Q149;
            Q149=makeQuery(id+"F9.opPattern","COPY",BODY,{"derivedFrom":makeQuery(id+"F8.opPattern","COPY",BODY,{"derivedFrom":makeQuery(id+"F5.opPattern","COPY",BODY,{"derivedFrom":makeQuery(id+"F1.opRevolve","SWEPT_BODY",BODY,{"disambiguationData":[OSD([sQuery(id+"F0.wireOp",EDGE,"E1")])]}),"instanceName":"1"}),"instanceName":"1"}),"instanceName":"1"});
            var Q150;
            Q150=makeQuery(id+"F9.opPattern","COPY",BODY,{"derivedFrom":makeQuery(id+"F8.opPattern","COPY",BODY,{"derivedFrom":makeQuery(id+"F5.opPattern","COPY",BODY,{"derivedFrom":makeQuery(id+"F2.opPattern","COPY",BODY,{"derivedFrom":makeQuery(id+"F1.opRevolve","SWEPT_BODY",BODY,{"disambiguationData":[OSD([sQuery(id+"F0.wireOp",EDGE,"E1")])]}),"instanceName":"1"}),"instanceName":"1"}),"instanceName":"1"}),"instanceName":"1"});
            var Q151;
            Q151=makeQuery(id+"F9.opPattern","COPY",BODY,{"derivedFrom":makeQuery(id+"F8.opPattern","COPY",BODY,{"derivedFrom":makeQuery(id+"F5.opPattern","COPY",BODY,{"derivedFrom":makeQuery(id+"F3.opPattern","COPY",BODY,{"derivedFrom":makeQuery(id+"F2.opPattern","COPY",BODY,{"derivedFrom":makeQuery(id+"F1.opRevolve","SWEPT_BODY",BODY,{"disambiguationData":[OSD([sQuery(id+"F0.wireOp",EDGE,"E1")])]}),"instanceName":"1"}),"instanceName":"1"}),"instanceName":"1"}),"instanceName":"1"}),"instanceName":"1"});
            var Q152;
            Q152=makeQuery(id+"F9.opPattern","COPY",BODY,{"derivedFrom":makeQuery(id+"F8.opPattern","COPY",BODY,{"derivedFrom":makeQuery(id+"F5.opPattern","COPY",BODY,{"derivedFrom":makeQuery(id+"F4.opPattern","COPY",BODY,{"derivedFrom":makeQuery(id+"F1.opRevolve","SWEPT_BODY",BODY,{"disambiguationData":[OSD([sQuery(id+"F0.wireOp",EDGE,"E1")])]}),"instanceName":"1"}),"instanceName":"1"}),"instanceName":"1"}),"instanceName":"1"});
            var Q153;
            Q153=makeQuery(id+"F9.opPattern","COPY",BODY,{"derivedFrom":makeQuery(id+"F8.opPattern","COPY",BODY,{"derivedFrom":makeQuery(id+"F5.opPattern","COPY",BODY,{"derivedFrom":makeQuery(id+"F4.opPattern","COPY",BODY,{"derivedFrom":makeQuery(id+"F2.opPattern","COPY",BODY,{"derivedFrom":makeQuery(id+"F1.opRevolve","SWEPT_BODY",BODY,{"disambiguationData":[OSD([sQuery(id+"F0.wireOp",EDGE,"E1")])]}),"instanceName":"1"}),"instanceName":"1"}),"instanceName":"1"}),"instanceName":"1"}),"instanceName":"1"});
            var Q154;
            Q154=makeQuery(id+"F9.opPattern","COPY",BODY,{"derivedFrom":makeQuery(id+"F8.opPattern","COPY",BODY,{"derivedFrom":makeQuery(id+"F5.opPattern","COPY",BODY,{"derivedFrom":makeQuery(id+"F4.opPattern","COPY",BODY,{"derivedFrom":makeQuery(id+"F3.opPattern","COPY",BODY,{"derivedFrom":makeQuery(id+"F2.opPattern","COPY",BODY,{"derivedFrom":makeQuery(id+"F1.opRevolve","SWEPT_BODY",BODY,{"disambiguationData":[OSD([sQuery(id+"F0.wireOp",EDGE,"E1")])]}),"instanceName":"1"}),"instanceName":"1"}),"instanceName":"1"}),"instanceName":"1"}),"instanceName":"1"}),"instanceName":"1"});
            var Q155;
            Q155=makeQuery(id+"F9.opPattern","COPY",BODY,{"derivedFrom":makeQuery(id+"F8.opPattern","COPY",BODY,{"derivedFrom":makeQuery(id+"F6.opPattern","COPY",BODY,{"derivedFrom":makeQuery(id+"F1.opRevolve","SWEPT_BODY",BODY,{"disambiguationData":[OSD([sQuery(id+"F0.wireOp",EDGE,"E1")])]}),"instanceName":"1"}),"instanceName":"1"}),"instanceName":"1"});
            var Q156;
            Q156=makeQuery(id+"F9.opPattern","COPY",BODY,{"derivedFrom":makeQuery(id+"F8.opPattern","COPY",BODY,{"derivedFrom":makeQuery(id+"F6.opPattern","COPY",BODY,{"derivedFrom":makeQuery(id+"F2.opPattern","COPY",BODY,{"derivedFrom":makeQuery(id+"F1.opRevolve","SWEPT_BODY",BODY,{"disambiguationData":[OSD([sQuery(id+"F0.wireOp",EDGE,"E1")])]}),"instanceName":"1"}),"instanceName":"1"}),"instanceName":"1"}),"instanceName":"1"});
            var Q157;
            Q157=makeQuery(id+"F9.opPattern","COPY",BODY,{"derivedFrom":makeQuery(id+"F8.opPattern","COPY",BODY,{"derivedFrom":makeQuery(id+"F6.opPattern","COPY",BODY,{"derivedFrom":makeQuery(id+"F3.opPattern","COPY",BODY,{"derivedFrom":makeQuery(id+"F2.opPattern","COPY",BODY,{"derivedFrom":makeQuery(id+"F1.opRevolve","SWEPT_BODY",BODY,{"disambiguationData":[OSD([sQuery(id+"F0.wireOp",EDGE,"E1")])]}),"instanceName":"1"}),"instanceName":"1"}),"instanceName":"1"}),"instanceName":"1"}),"instanceName":"1"});
            var Q158;
            Q158=makeQuery(id+"F9.opPattern","COPY",BODY,{"derivedFrom":makeQuery(id+"F8.opPattern","COPY",BODY,{"derivedFrom":makeQuery(id+"F6.opPattern","COPY",BODY,{"derivedFrom":makeQuery(id+"F4.opPattern","COPY",BODY,{"derivedFrom":makeQuery(id+"F1.opRevolve","SWEPT_BODY",BODY,{"disambiguationData":[OSD([sQuery(id+"F0.wireOp",EDGE,"E1")])]}),"instanceName":"1"}),"instanceName":"1"}),"instanceName":"1"}),"instanceName":"1"});
            var Q159;
            Q159=makeQuery(id+"F9.opPattern","COPY",BODY,{"derivedFrom":makeQuery(id+"F8.opPattern","COPY",BODY,{"derivedFrom":makeQuery(id+"F6.opPattern","COPY",BODY,{"derivedFrom":makeQuery(id+"F4.opPattern","COPY",BODY,{"derivedFrom":makeQuery(id+"F2.opPattern","COPY",BODY,{"derivedFrom":makeQuery(id+"F1.opRevolve","SWEPT_BODY",BODY,{"disambiguationData":[OSD([sQuery(id+"F0.wireOp",EDGE,"E1")])]}),"instanceName":"1"}),"instanceName":"1"}),"instanceName":"1"}),"instanceName":"1"}),"instanceName":"1"});
            var Q160;
            Q160=makeQuery(id+"F9.opPattern","COPY",BODY,{"derivedFrom":makeQuery(id+"F8.opPattern","COPY",BODY,{"derivedFrom":makeQuery(id+"F6.opPattern","COPY",BODY,{"derivedFrom":makeQuery(id+"F4.opPattern","COPY",BODY,{"derivedFrom":makeQuery(id+"F3.opPattern","COPY",BODY,{"derivedFrom":makeQuery(id+"F2.opPattern","COPY",BODY,{"derivedFrom":makeQuery(id+"F1.opRevolve","SWEPT_BODY",BODY,{"disambiguationData":[OSD([sQuery(id+"F0.wireOp",EDGE,"E1")])]}),"instanceName":"1"}),"instanceName":"1"}),"instanceName":"1"}),"instanceName":"1"}),"instanceName":"1"}),"instanceName":"1"});
            var Q161;
            Q161=makeQuery(id+"F9.opPattern","COPY",BODY,{"derivedFrom":makeQuery(id+"F8.opPattern","COPY",BODY,{"derivedFrom":makeQuery(id+"F6.opPattern","COPY",BODY,{"derivedFrom":makeQuery(id+"F5.opPattern","COPY",BODY,{"derivedFrom":makeQuery(id+"F1.opRevolve","SWEPT_BODY",BODY,{"disambiguationData":[OSD([sQuery(id+"F0.wireOp",EDGE,"E1")])]}),"instanceName":"1"}),"instanceName":"1"}),"instanceName":"1"}),"instanceName":"1"});
            var Q162;
            Q162=makeQuery(id+"F9.opPattern","COPY",BODY,{"derivedFrom":makeQuery(id+"F8.opPattern","COPY",BODY,{"derivedFrom":makeQuery(id+"F6.opPattern","COPY",BODY,{"derivedFrom":makeQuery(id+"F5.opPattern","COPY",BODY,{"derivedFrom":makeQuery(id+"F2.opPattern","COPY",BODY,{"derivedFrom":makeQuery(id+"F1.opRevolve","SWEPT_BODY",BODY,{"disambiguationData":[OSD([sQuery(id+"F0.wireOp",EDGE,"E1")])]}),"instanceName":"1"}),"instanceName":"1"}),"instanceName":"1"}),"instanceName":"1"}),"instanceName":"1"});
            var Q163;
            Q163=makeQuery(id+"F9.opPattern","COPY",BODY,{"derivedFrom":makeQuery(id+"F8.opPattern","COPY",BODY,{"derivedFrom":makeQuery(id+"F6.opPattern","COPY",BODY,{"derivedFrom":makeQuery(id+"F5.opPattern","COPY",BODY,{"derivedFrom":makeQuery(id+"F3.opPattern","COPY",BODY,{"derivedFrom":makeQuery(id+"F2.opPattern","COPY",BODY,{"derivedFrom":makeQuery(id+"F1.opRevolve","SWEPT_BODY",BODY,{"disambiguationData":[OSD([sQuery(id+"F0.wireOp",EDGE,"E1")])]}),"instanceName":"1"}),"instanceName":"1"}),"instanceName":"1"}),"instanceName":"1"}),"instanceName":"1"}),"instanceName":"1"});
            var Q164;
            Q164=makeQuery(id+"F9.opPattern","COPY",BODY,{"derivedFrom":makeQuery(id+"F8.opPattern","COPY",BODY,{"derivedFrom":makeQuery(id+"F6.opPattern","COPY",BODY,{"derivedFrom":makeQuery(id+"F5.opPattern","COPY",BODY,{"derivedFrom":makeQuery(id+"F4.opPattern","COPY",BODY,{"derivedFrom":makeQuery(id+"F1.opRevolve","SWEPT_BODY",BODY,{"disambiguationData":[OSD([sQuery(id+"F0.wireOp",EDGE,"E1")])]}),"instanceName":"1"}),"instanceName":"1"}),"instanceName":"1"}),"instanceName":"1"}),"instanceName":"1"});
            var Q165;
            Q165=makeQuery(id+"F9.opPattern","COPY",BODY,{"derivedFrom":makeQuery(id+"F8.opPattern","COPY",BODY,{"derivedFrom":makeQuery(id+"F6.opPattern","COPY",BODY,{"derivedFrom":makeQuery(id+"F5.opPattern","COPY",BODY,{"derivedFrom":makeQuery(id+"F4.opPattern","COPY",BODY,{"derivedFrom":makeQuery(id+"F2.opPattern","COPY",BODY,{"derivedFrom":makeQuery(id+"F1.opRevolve","SWEPT_BODY",BODY,{"disambiguationData":[OSD([sQuery(id+"F0.wireOp",EDGE,"E1")])]}),"instanceName":"1"}),"instanceName":"1"}),"instanceName":"1"}),"instanceName":"1"}),"instanceName":"1"}),"instanceName":"1"});
            var Q166;
            Q166=makeQuery(id+"F9.opPattern","COPY",BODY,{"derivedFrom":makeQuery(id+"F8.opPattern","COPY",BODY,{"derivedFrom":makeQuery(id+"F6.opPattern","COPY",BODY,{"derivedFrom":makeQuery(id+"F5.opPattern","COPY",BODY,{"derivedFrom":makeQuery(id+"F4.opPattern","COPY",BODY,{"derivedFrom":makeQuery(id+"F3.opPattern","COPY",BODY,{"derivedFrom":makeQuery(id+"F2.opPattern","COPY",BODY,{"derivedFrom":makeQuery(id+"F1.opRevolve","SWEPT_BODY",BODY,{"disambiguationData":[OSD([sQuery(id+"F0.wireOp",EDGE,"E1")])]}),"instanceName":"1"}),"instanceName":"1"}),"instanceName":"1"}),"instanceName":"1"}),"instanceName":"1"}),"instanceName":"1"}),"instanceName":"1"});
            var Q167;
            Q167=makeQuery(id+"F9.opPattern","COPY",BODY,{"derivedFrom":makeQuery(id+"F8.opPattern","COPY",BODY,{"derivedFrom":makeQuery(id+"F7.opPattern","COPY",BODY,{"derivedFrom":makeQuery(id+"F1.opRevolve","SWEPT_BODY",BODY,{"disambiguationData":[OSD([sQuery(id+"F0.wireOp",EDGE,"E1")])]}),"instanceName":"1"}),"instanceName":"1"}),"instanceName":"1"});
            var Q168;
            Q168=makeQuery(id+"F9.opPattern","COPY",BODY,{"derivedFrom":makeQuery(id+"F8.opPattern","COPY",BODY,{"derivedFrom":makeQuery(id+"F7.opPattern","COPY",BODY,{"derivedFrom":makeQuery(id+"F2.opPattern","COPY",BODY,{"derivedFrom":makeQuery(id+"F1.opRevolve","SWEPT_BODY",BODY,{"disambiguationData":[OSD([sQuery(id+"F0.wireOp",EDGE,"E1")])]}),"instanceName":"1"}),"instanceName":"1"}),"instanceName":"1"}),"instanceName":"1"});
            var Q169;
            Q169=makeQuery(id+"F9.opPattern","COPY",BODY,{"derivedFrom":makeQuery(id+"F8.opPattern","COPY",BODY,{"derivedFrom":makeQuery(id+"F7.opPattern","COPY",BODY,{"derivedFrom":makeQuery(id+"F3.opPattern","COPY",BODY,{"derivedFrom":makeQuery(id+"F2.opPattern","COPY",BODY,{"derivedFrom":makeQuery(id+"F1.opRevolve","SWEPT_BODY",BODY,{"disambiguationData":[OSD([sQuery(id+"F0.wireOp",EDGE,"E1")])]}),"instanceName":"1"}),"instanceName":"1"}),"instanceName":"1"}),"instanceName":"1"}),"instanceName":"1"});
            var Q170;
            Q170=makeQuery(id+"F9.opPattern","COPY",BODY,{"derivedFrom":makeQuery(id+"F8.opPattern","COPY",BODY,{"derivedFrom":makeQuery(id+"F7.opPattern","COPY",BODY,{"derivedFrom":makeQuery(id+"F4.opPattern","COPY",BODY,{"derivedFrom":makeQuery(id+"F1.opRevolve","SWEPT_BODY",BODY,{"disambiguationData":[OSD([sQuery(id+"F0.wireOp",EDGE,"E1")])]}),"instanceName":"1"}),"instanceName":"1"}),"instanceName":"1"}),"instanceName":"1"});
            var Q171;
            Q171=makeQuery(id+"F9.opPattern","COPY",BODY,{"derivedFrom":makeQuery(id+"F8.opPattern","COPY",BODY,{"derivedFrom":makeQuery(id+"F7.opPattern","COPY",BODY,{"derivedFrom":makeQuery(id+"F4.opPattern","COPY",BODY,{"derivedFrom":makeQuery(id+"F2.opPattern","COPY",BODY,{"derivedFrom":makeQuery(id+"F1.opRevolve","SWEPT_BODY",BODY,{"disambiguationData":[OSD([sQuery(id+"F0.wireOp",EDGE,"E1")])]}),"instanceName":"1"}),"instanceName":"1"}),"instanceName":"1"}),"instanceName":"1"}),"instanceName":"1"});
            var Q172;
            Q172=makeQuery(id+"F9.opPattern","COPY",BODY,{"derivedFrom":makeQuery(id+"F8.opPattern","COPY",BODY,{"derivedFrom":makeQuery(id+"F7.opPattern","COPY",BODY,{"derivedFrom":makeQuery(id+"F4.opPattern","COPY",BODY,{"derivedFrom":makeQuery(id+"F3.opPattern","COPY",BODY,{"derivedFrom":makeQuery(id+"F2.opPattern","COPY",BODY,{"derivedFrom":makeQuery(id+"F1.opRevolve","SWEPT_BODY",BODY,{"disambiguationData":[OSD([sQuery(id+"F0.wireOp",EDGE,"E1")])]}),"instanceName":"1"}),"instanceName":"1"}),"instanceName":"1"}),"instanceName":"1"}),"instanceName":"1"}),"instanceName":"1"});
            var Q173;
            Q173=makeQuery(id+"F9.opPattern","COPY",BODY,{"derivedFrom":makeQuery(id+"F8.opPattern","COPY",BODY,{"derivedFrom":makeQuery(id+"F7.opPattern","COPY",BODY,{"derivedFrom":makeQuery(id+"F5.opPattern","COPY",BODY,{"derivedFrom":makeQuery(id+"F1.opRevolve","SWEPT_BODY",BODY,{"disambiguationData":[OSD([sQuery(id+"F0.wireOp",EDGE,"E1")])]}),"instanceName":"1"}),"instanceName":"1"}),"instanceName":"1"}),"instanceName":"1"});
            var Q174;
            Q174=makeQuery(id+"F9.opPattern","COPY",BODY,{"derivedFrom":makeQuery(id+"F8.opPattern","COPY",BODY,{"derivedFrom":makeQuery(id+"F7.opPattern","COPY",BODY,{"derivedFrom":makeQuery(id+"F5.opPattern","COPY",BODY,{"derivedFrom":makeQuery(id+"F2.opPattern","COPY",BODY,{"derivedFrom":makeQuery(id+"F1.opRevolve","SWEPT_BODY",BODY,{"disambiguationData":[OSD([sQuery(id+"F0.wireOp",EDGE,"E1")])]}),"instanceName":"1"}),"instanceName":"1"}),"instanceName":"1"}),"instanceName":"1"}),"instanceName":"1"});
            var Q175;
            Q175=makeQuery(id+"F9.opPattern","COPY",BODY,{"derivedFrom":makeQuery(id+"F8.opPattern","COPY",BODY,{"derivedFrom":makeQuery(id+"F7.opPattern","COPY",BODY,{"derivedFrom":makeQuery(id+"F5.opPattern","COPY",BODY,{"derivedFrom":makeQuery(id+"F3.opPattern","COPY",BODY,{"derivedFrom":makeQuery(id+"F2.opPattern","COPY",BODY,{"derivedFrom":makeQuery(id+"F1.opRevolve","SWEPT_BODY",BODY,{"disambiguationData":[OSD([sQuery(id+"F0.wireOp",EDGE,"E1")])]}),"instanceName":"1"}),"instanceName":"1"}),"instanceName":"1"}),"instanceName":"1"}),"instanceName":"1"}),"instanceName":"1"});
            var Q176;
            Q176=makeQuery(id+"F9.opPattern","COPY",BODY,{"derivedFrom":makeQuery(id+"F8.opPattern","COPY",BODY,{"derivedFrom":makeQuery(id+"F7.opPattern","COPY",BODY,{"derivedFrom":makeQuery(id+"F5.opPattern","COPY",BODY,{"derivedFrom":makeQuery(id+"F4.opPattern","COPY",BODY,{"derivedFrom":makeQuery(id+"F1.opRevolve","SWEPT_BODY",BODY,{"disambiguationData":[OSD([sQuery(id+"F0.wireOp",EDGE,"E1")])]}),"instanceName":"1"}),"instanceName":"1"}),"instanceName":"1"}),"instanceName":"1"}),"instanceName":"1"});
            var Q177;
            Q177=makeQuery(id+"F9.opPattern","COPY",BODY,{"derivedFrom":makeQuery(id+"F8.opPattern","COPY",BODY,{"derivedFrom":makeQuery(id+"F7.opPattern","COPY",BODY,{"derivedFrom":makeQuery(id+"F5.opPattern","COPY",BODY,{"derivedFrom":makeQuery(id+"F4.opPattern","COPY",BODY,{"derivedFrom":makeQuery(id+"F2.opPattern","COPY",BODY,{"derivedFrom":makeQuery(id+"F1.opRevolve","SWEPT_BODY",BODY,{"disambiguationData":[OSD([sQuery(id+"F0.wireOp",EDGE,"E1")])]}),"instanceName":"1"}),"instanceName":"1"}),"instanceName":"1"}),"instanceName":"1"}),"instanceName":"1"}),"instanceName":"1"});
            var Q178;
            Q178=makeQuery(id+"F9.opPattern","COPY",BODY,{"derivedFrom":makeQuery(id+"F8.opPattern","COPY",BODY,{"derivedFrom":makeQuery(id+"F7.opPattern","COPY",BODY,{"derivedFrom":makeQuery(id+"F5.opPattern","COPY",BODY,{"derivedFrom":makeQuery(id+"F4.opPattern","COPY",BODY,{"derivedFrom":makeQuery(id+"F3.opPattern","COPY",BODY,{"derivedFrom":makeQuery(id+"F2.opPattern","COPY",BODY,{"derivedFrom":makeQuery(id+"F1.opRevolve","SWEPT_BODY",BODY,{"disambiguationData":[OSD([sQuery(id+"F0.wireOp",EDGE,"E1")])]}),"instanceName":"1"}),"instanceName":"1"}),"instanceName":"1"}),"instanceName":"1"}),"instanceName":"1"}),"instanceName":"1"}),"instanceName":"1"});
            var Q179;
            Q179=makeQuery(id+"F9.opPattern","COPY",BODY,{"derivedFrom":makeQuery(id+"F8.opPattern","COPY",BODY,{"derivedFrom":makeQuery(id+"F7.opPattern","COPY",BODY,{"derivedFrom":makeQuery(id+"F6.opPattern","COPY",BODY,{"derivedFrom":makeQuery(id+"F1.opRevolve","SWEPT_BODY",BODY,{"disambiguationData":[OSD([sQuery(id+"F0.wireOp",EDGE,"E1")])]}),"instanceName":"1"}),"instanceName":"1"}),"instanceName":"1"}),"instanceName":"1"});
            var Q180;
            Q180=makeQuery(id+"F9.opPattern","COPY",BODY,{"derivedFrom":makeQuery(id+"F8.opPattern","COPY",BODY,{"derivedFrom":makeQuery(id+"F7.opPattern","COPY",BODY,{"derivedFrom":makeQuery(id+"F6.opPattern","COPY",BODY,{"derivedFrom":makeQuery(id+"F2.opPattern","COPY",BODY,{"derivedFrom":makeQuery(id+"F1.opRevolve","SWEPT_BODY",BODY,{"disambiguationData":[OSD([sQuery(id+"F0.wireOp",EDGE,"E1")])]}),"instanceName":"1"}),"instanceName":"1"}),"instanceName":"1"}),"instanceName":"1"}),"instanceName":"1"});
            var Q181;
            Q181=makeQuery(id+"F9.opPattern","COPY",BODY,{"derivedFrom":makeQuery(id+"F8.opPattern","COPY",BODY,{"derivedFrom":makeQuery(id+"F7.opPattern","COPY",BODY,{"derivedFrom":makeQuery(id+"F6.opPattern","COPY",BODY,{"derivedFrom":makeQuery(id+"F3.opPattern","COPY",BODY,{"derivedFrom":makeQuery(id+"F2.opPattern","COPY",BODY,{"derivedFrom":makeQuery(id+"F1.opRevolve","SWEPT_BODY",BODY,{"disambiguationData":[OSD([sQuery(id+"F0.wireOp",EDGE,"E1")])]}),"instanceName":"1"}),"instanceName":"1"}),"instanceName":"1"}),"instanceName":"1"}),"instanceName":"1"}),"instanceName":"1"});
            var Q182;
            Q182=makeQuery(id+"F9.opPattern","COPY",BODY,{"derivedFrom":makeQuery(id+"F8.opPattern","COPY",BODY,{"derivedFrom":makeQuery(id+"F7.opPattern","COPY",BODY,{"derivedFrom":makeQuery(id+"F6.opPattern","COPY",BODY,{"derivedFrom":makeQuery(id+"F4.opPattern","COPY",BODY,{"derivedFrom":makeQuery(id+"F1.opRevolve","SWEPT_BODY",BODY,{"disambiguationData":[OSD([sQuery(id+"F0.wireOp",EDGE,"E1")])]}),"instanceName":"1"}),"instanceName":"1"}),"instanceName":"1"}),"instanceName":"1"}),"instanceName":"1"});
            var Q183;
            Q183=makeQuery(id+"F9.opPattern","COPY",BODY,{"derivedFrom":makeQuery(id+"F8.opPattern","COPY",BODY,{"derivedFrom":makeQuery(id+"F7.opPattern","COPY",BODY,{"derivedFrom":makeQuery(id+"F6.opPattern","COPY",BODY,{"derivedFrom":makeQuery(id+"F4.opPattern","COPY",BODY,{"derivedFrom":makeQuery(id+"F2.opPattern","COPY",BODY,{"derivedFrom":makeQuery(id+"F1.opRevolve","SWEPT_BODY",BODY,{"disambiguationData":[OSD([sQuery(id+"F0.wireOp",EDGE,"E1")])]}),"instanceName":"1"}),"instanceName":"1"}),"instanceName":"1"}),"instanceName":"1"}),"instanceName":"1"}),"instanceName":"1"});
            var Q184;
            Q184=makeQuery(id+"F9.opPattern","COPY",BODY,{"derivedFrom":makeQuery(id+"F8.opPattern","COPY",BODY,{"derivedFrom":makeQuery(id+"F7.opPattern","COPY",BODY,{"derivedFrom":makeQuery(id+"F6.opPattern","COPY",BODY,{"derivedFrom":makeQuery(id+"F4.opPattern","COPY",BODY,{"derivedFrom":makeQuery(id+"F3.opPattern","COPY",BODY,{"derivedFrom":makeQuery(id+"F2.opPattern","COPY",BODY,{"derivedFrom":makeQuery(id+"F1.opRevolve","SWEPT_BODY",BODY,{"disambiguationData":[OSD([sQuery(id+"F0.wireOp",EDGE,"E1")])]}),"instanceName":"1"}),"instanceName":"1"}),"instanceName":"1"}),"instanceName":"1"}),"instanceName":"1"}),"instanceName":"1"}),"instanceName":"1"});
            var Q185;
            Q185=makeQuery(id+"F9.opPattern","COPY",BODY,{"derivedFrom":makeQuery(id+"F8.opPattern","COPY",BODY,{"derivedFrom":makeQuery(id+"F7.opPattern","COPY",BODY,{"derivedFrom":makeQuery(id+"F6.opPattern","COPY",BODY,{"derivedFrom":makeQuery(id+"F5.opPattern","COPY",BODY,{"derivedFrom":makeQuery(id+"F1.opRevolve","SWEPT_BODY",BODY,{"disambiguationData":[OSD([sQuery(id+"F0.wireOp",EDGE,"E1")])]}),"instanceName":"1"}),"instanceName":"1"}),"instanceName":"1"}),"instanceName":"1"}),"instanceName":"1"});
            var Q186;
            Q186=makeQuery(id+"F9.opPattern","COPY",BODY,{"derivedFrom":makeQuery(id+"F8.opPattern","COPY",BODY,{"derivedFrom":makeQuery(id+"F7.opPattern","COPY",BODY,{"derivedFrom":makeQuery(id+"F6.opPattern","COPY",BODY,{"derivedFrom":makeQuery(id+"F5.opPattern","COPY",BODY,{"derivedFrom":makeQuery(id+"F2.opPattern","COPY",BODY,{"derivedFrom":makeQuery(id+"F1.opRevolve","SWEPT_BODY",BODY,{"disambiguationData":[OSD([sQuery(id+"F0.wireOp",EDGE,"E1")])]}),"instanceName":"1"}),"instanceName":"1"}),"instanceName":"1"}),"instanceName":"1"}),"instanceName":"1"}),"instanceName":"1"});
            var Q187;
            Q187=makeQuery(id+"F9.opPattern","COPY",BODY,{"derivedFrom":makeQuery(id+"F8.opPattern","COPY",BODY,{"derivedFrom":makeQuery(id+"F7.opPattern","COPY",BODY,{"derivedFrom":makeQuery(id+"F6.opPattern","COPY",BODY,{"derivedFrom":makeQuery(id+"F5.opPattern","COPY",BODY,{"derivedFrom":makeQuery(id+"F3.opPattern","COPY",BODY,{"derivedFrom":makeQuery(id+"F2.opPattern","COPY",BODY,{"derivedFrom":makeQuery(id+"F1.opRevolve","SWEPT_BODY",BODY,{"disambiguationData":[OSD([sQuery(id+"F0.wireOp",EDGE,"E1")])]}),"instanceName":"1"}),"instanceName":"1"}),"instanceName":"1"}),"instanceName":"1"}),"instanceName":"1"}),"instanceName":"1"}),"instanceName":"1"});
            var Q188;
            Q188=makeQuery(id+"F9.opPattern","COPY",BODY,{"derivedFrom":makeQuery(id+"F8.opPattern","COPY",BODY,{"derivedFrom":makeQuery(id+"F7.opPattern","COPY",BODY,{"derivedFrom":makeQuery(id+"F6.opPattern","COPY",BODY,{"derivedFrom":makeQuery(id+"F5.opPattern","COPY",BODY,{"derivedFrom":makeQuery(id+"F4.opPattern","COPY",BODY,{"derivedFrom":makeQuery(id+"F1.opRevolve","SWEPT_BODY",BODY,{"disambiguationData":[OSD([sQuery(id+"F0.wireOp",EDGE,"E1")])]}),"instanceName":"1"}),"instanceName":"1"}),"instanceName":"1"}),"instanceName":"1"}),"instanceName":"1"}),"instanceName":"1"});
            var Q189;
            Q189=makeQuery(id+"F9.opPattern","COPY",BODY,{"derivedFrom":makeQuery(id+"F8.opPattern","COPY",BODY,{"derivedFrom":makeQuery(id+"F7.opPattern","COPY",BODY,{"derivedFrom":makeQuery(id+"F6.opPattern","COPY",BODY,{"derivedFrom":makeQuery(id+"F5.opPattern","COPY",BODY,{"derivedFrom":makeQuery(id+"F4.opPattern","COPY",BODY,{"derivedFrom":makeQuery(id+"F2.opPattern","COPY",BODY,{"derivedFrom":makeQuery(id+"F1.opRevolve","SWEPT_BODY",BODY,{"disambiguationData":[OSD([sQuery(id+"F0.wireOp",EDGE,"E1")])]}),"instanceName":"1"}),"instanceName":"1"}),"instanceName":"1"}),"instanceName":"1"}),"instanceName":"1"}),"instanceName":"1"}),"instanceName":"1"});
            var Q190;
            Q190=makeQuery(id+"F9.opPattern","COPY",BODY,{"derivedFrom":makeQuery(id+"F8.opPattern","COPY",BODY,{"derivedFrom":makeQuery(id+"F7.opPattern","COPY",BODY,{"derivedFrom":makeQuery(id+"F6.opPattern","COPY",BODY,{"derivedFrom":makeQuery(id+"F5.opPattern","COPY",BODY,{"derivedFrom":makeQuery(id+"F4.opPattern","COPY",BODY,{"derivedFrom":makeQuery(id+"F3.opPattern","COPY",BODY,{"derivedFrom":makeQuery(id+"F2.opPattern","COPY",BODY,{"derivedFrom":makeQuery(id+"F1.opRevolve","SWEPT_BODY",BODY,{"disambiguationData":[OSD([sQuery(id+"F0.wireOp",EDGE,"E1")])]}),"instanceName":"1"}),"instanceName":"1"}),"instanceName":"1"}),"instanceName":"1"}),"instanceName":"1"}),"instanceName":"1"}),"instanceName":"1"}),"instanceName":"1"});
            var Q191;
            Q191=makeQuery(id+"F10.opPattern","COPY",BODY,{"derivedFrom":makeQuery(id+"F1.opRevolve","SWEPT_BODY",BODY,{"disambiguationData":[OSD([sQuery(id+"F0.wireOp",EDGE,"E1")])]}),"instanceName":"1"});
            var Q192;
            Q192=makeQuery(id+"F10.opPattern","COPY",BODY,{"derivedFrom":makeQuery(id+"F2.opPattern","COPY",BODY,{"derivedFrom":makeQuery(id+"F1.opRevolve","SWEPT_BODY",BODY,{"disambiguationData":[OSD([sQuery(id+"F0.wireOp",EDGE,"E1")])]}),"instanceName":"1"}),"instanceName":"1"});
            var Q193;
            Q193=makeQuery(id+"F10.opPattern","COPY",BODY,{"derivedFrom":makeQuery(id+"F3.opPattern","COPY",BODY,{"derivedFrom":makeQuery(id+"F2.opPattern","COPY",BODY,{"derivedFrom":makeQuery(id+"F1.opRevolve","SWEPT_BODY",BODY,{"disambiguationData":[OSD([sQuery(id+"F0.wireOp",EDGE,"E1")])]}),"instanceName":"1"}),"instanceName":"1"}),"instanceName":"1"});
            var Q194;
            Q194=makeQuery(id+"F10.opPattern","COPY",BODY,{"derivedFrom":makeQuery(id+"F4.opPattern","COPY",BODY,{"derivedFrom":makeQuery(id+"F1.opRevolve","SWEPT_BODY",BODY,{"disambiguationData":[OSD([sQuery(id+"F0.wireOp",EDGE,"E1")])]}),"instanceName":"1"}),"instanceName":"1"});
            var Q195;
            Q195=makeQuery(id+"F10.opPattern","COPY",BODY,{"derivedFrom":makeQuery(id+"F4.opPattern","COPY",BODY,{"derivedFrom":makeQuery(id+"F2.opPattern","COPY",BODY,{"derivedFrom":makeQuery(id+"F1.opRevolve","SWEPT_BODY",BODY,{"disambiguationData":[OSD([sQuery(id+"F0.wireOp",EDGE,"E1")])]}),"instanceName":"1"}),"instanceName":"1"}),"instanceName":"1"});
            var Q196;
            Q196=makeQuery(id+"F10.opPattern","COPY",BODY,{"derivedFrom":makeQuery(id+"F4.opPattern","COPY",BODY,{"derivedFrom":makeQuery(id+"F3.opPattern","COPY",BODY,{"derivedFrom":makeQuery(id+"F2.opPattern","COPY",BODY,{"derivedFrom":makeQuery(id+"F1.opRevolve","SWEPT_BODY",BODY,{"disambiguationData":[OSD([sQuery(id+"F0.wireOp",EDGE,"E1")])]}),"instanceName":"1"}),"instanceName":"1"}),"instanceName":"1"}),"instanceName":"1"});
            var Q197;
            Q197=makeQuery(id+"F10.opPattern","COPY",BODY,{"derivedFrom":makeQuery(id+"F5.opPattern","COPY",BODY,{"derivedFrom":makeQuery(id+"F1.opRevolve","SWEPT_BODY",BODY,{"disambiguationData":[OSD([sQuery(id+"F0.wireOp",EDGE,"E1")])]}),"instanceName":"1"}),"instanceName":"1"});
            var Q198;
            Q198=makeQuery(id+"F10.opPattern","COPY",BODY,{"derivedFrom":makeQuery(id+"F5.opPattern","COPY",BODY,{"derivedFrom":makeQuery(id+"F2.opPattern","COPY",BODY,{"derivedFrom":makeQuery(id+"F1.opRevolve","SWEPT_BODY",BODY,{"disambiguationData":[OSD([sQuery(id+"F0.wireOp",EDGE,"E1")])]}),"instanceName":"1"}),"instanceName":"1"}),"instanceName":"1"});
            var Q199;
            Q199=makeQuery(id+"F10.opPattern","COPY",BODY,{"derivedFrom":makeQuery(id+"F5.opPattern","COPY",BODY,{"derivedFrom":makeQuery(id+"F3.opPattern","COPY",BODY,{"derivedFrom":makeQuery(id+"F2.opPattern","COPY",BODY,{"derivedFrom":makeQuery(id+"F1.opRevolve","SWEPT_BODY",BODY,{"disambiguationData":[OSD([sQuery(id+"F0.wireOp",EDGE,"E1")])]}),"instanceName":"1"}),"instanceName":"1"}),"instanceName":"1"}),"instanceName":"1"});
            var Q200;
            Q200=makeQuery(id+"F10.opPattern","COPY",BODY,{"derivedFrom":makeQuery(id+"F5.opPattern","COPY",BODY,{"derivedFrom":makeQuery(id+"F4.opPattern","COPY",BODY,{"derivedFrom":makeQuery(id+"F1.opRevolve","SWEPT_BODY",BODY,{"disambiguationData":[OSD([sQuery(id+"F0.wireOp",EDGE,"E1")])]}),"instanceName":"1"}),"instanceName":"1"}),"instanceName":"1"});
            var Q201;
            Q201=makeQuery(id+"F10.opPattern","COPY",BODY,{"derivedFrom":makeQuery(id+"F5.opPattern","COPY",BODY,{"derivedFrom":makeQuery(id+"F4.opPattern","COPY",BODY,{"derivedFrom":makeQuery(id+"F2.opPattern","COPY",BODY,{"derivedFrom":makeQuery(id+"F1.opRevolve","SWEPT_BODY",BODY,{"disambiguationData":[OSD([sQuery(id+"F0.wireOp",EDGE,"E1")])]}),"instanceName":"1"}),"instanceName":"1"}),"instanceName":"1"}),"instanceName":"1"});
            var Q202;
            Q202=makeQuery(id+"F10.opPattern","COPY",BODY,{"derivedFrom":makeQuery(id+"F5.opPattern","COPY",BODY,{"derivedFrom":makeQuery(id+"F4.opPattern","COPY",BODY,{"derivedFrom":makeQuery(id+"F3.opPattern","COPY",BODY,{"derivedFrom":makeQuery(id+"F2.opPattern","COPY",BODY,{"derivedFrom":makeQuery(id+"F1.opRevolve","SWEPT_BODY",BODY,{"disambiguationData":[OSD([sQuery(id+"F0.wireOp",EDGE,"E1")])]}),"instanceName":"1"}),"instanceName":"1"}),"instanceName":"1"}),"instanceName":"1"}),"instanceName":"1"});
            var Q203;
            Q203=makeQuery(id+"F10.opPattern","COPY",BODY,{"derivedFrom":makeQuery(id+"F6.opPattern","COPY",BODY,{"derivedFrom":makeQuery(id+"F1.opRevolve","SWEPT_BODY",BODY,{"disambiguationData":[OSD([sQuery(id+"F0.wireOp",EDGE,"E1")])]}),"instanceName":"1"}),"instanceName":"1"});
            var Q204;
            Q204=makeQuery(id+"F10.opPattern","COPY",BODY,{"derivedFrom":makeQuery(id+"F6.opPattern","COPY",BODY,{"derivedFrom":makeQuery(id+"F2.opPattern","COPY",BODY,{"derivedFrom":makeQuery(id+"F1.opRevolve","SWEPT_BODY",BODY,{"disambiguationData":[OSD([sQuery(id+"F0.wireOp",EDGE,"E1")])]}),"instanceName":"1"}),"instanceName":"1"}),"instanceName":"1"});
            var Q205;
            Q205=makeQuery(id+"F10.opPattern","COPY",BODY,{"derivedFrom":makeQuery(id+"F6.opPattern","COPY",BODY,{"derivedFrom":makeQuery(id+"F3.opPattern","COPY",BODY,{"derivedFrom":makeQuery(id+"F2.opPattern","COPY",BODY,{"derivedFrom":makeQuery(id+"F1.opRevolve","SWEPT_BODY",BODY,{"disambiguationData":[OSD([sQuery(id+"F0.wireOp",EDGE,"E1")])]}),"instanceName":"1"}),"instanceName":"1"}),"instanceName":"1"}),"instanceName":"1"});
            var Q206;
            Q206=makeQuery(id+"F10.opPattern","COPY",BODY,{"derivedFrom":makeQuery(id+"F6.opPattern","COPY",BODY,{"derivedFrom":makeQuery(id+"F4.opPattern","COPY",BODY,{"derivedFrom":makeQuery(id+"F1.opRevolve","SWEPT_BODY",BODY,{"disambiguationData":[OSD([sQuery(id+"F0.wireOp",EDGE,"E1")])]}),"instanceName":"1"}),"instanceName":"1"}),"instanceName":"1"});
            var Q207;
            Q207=makeQuery(id+"F10.opPattern","COPY",BODY,{"derivedFrom":makeQuery(id+"F6.opPattern","COPY",BODY,{"derivedFrom":makeQuery(id+"F4.opPattern","COPY",BODY,{"derivedFrom":makeQuery(id+"F2.opPattern","COPY",BODY,{"derivedFrom":makeQuery(id+"F1.opRevolve","SWEPT_BODY",BODY,{"disambiguationData":[OSD([sQuery(id+"F0.wireOp",EDGE,"E1")])]}),"instanceName":"1"}),"instanceName":"1"}),"instanceName":"1"}),"instanceName":"1"});
            var Q208;
            Q208=makeQuery(id+"F10.opPattern","COPY",BODY,{"derivedFrom":makeQuery(id+"F6.opPattern","COPY",BODY,{"derivedFrom":makeQuery(id+"F4.opPattern","COPY",BODY,{"derivedFrom":makeQuery(id+"F3.opPattern","COPY",BODY,{"derivedFrom":makeQuery(id+"F2.opPattern","COPY",BODY,{"derivedFrom":makeQuery(id+"F1.opRevolve","SWEPT_BODY",BODY,{"disambiguationData":[OSD([sQuery(id+"F0.wireOp",EDGE,"E1")])]}),"instanceName":"1"}),"instanceName":"1"}),"instanceName":"1"}),"instanceName":"1"}),"instanceName":"1"});
            var Q209;
            Q209=makeQuery(id+"F10.opPattern","COPY",BODY,{"derivedFrom":makeQuery(id+"F6.opPattern","COPY",BODY,{"derivedFrom":makeQuery(id+"F5.opPattern","COPY",BODY,{"derivedFrom":makeQuery(id+"F1.opRevolve","SWEPT_BODY",BODY,{"disambiguationData":[OSD([sQuery(id+"F0.wireOp",EDGE,"E1")])]}),"instanceName":"1"}),"instanceName":"1"}),"instanceName":"1"});
            var Q210;
            Q210=makeQuery(id+"F10.opPattern","COPY",BODY,{"derivedFrom":makeQuery(id+"F6.opPattern","COPY",BODY,{"derivedFrom":makeQuery(id+"F5.opPattern","COPY",BODY,{"derivedFrom":makeQuery(id+"F2.opPattern","COPY",BODY,{"derivedFrom":makeQuery(id+"F1.opRevolve","SWEPT_BODY",BODY,{"disambiguationData":[OSD([sQuery(id+"F0.wireOp",EDGE,"E1")])]}),"instanceName":"1"}),"instanceName":"1"}),"instanceName":"1"}),"instanceName":"1"});
            var Q211;
            Q211=makeQuery(id+"F10.opPattern","COPY",BODY,{"derivedFrom":makeQuery(id+"F6.opPattern","COPY",BODY,{"derivedFrom":makeQuery(id+"F5.opPattern","COPY",BODY,{"derivedFrom":makeQuery(id+"F3.opPattern","COPY",BODY,{"derivedFrom":makeQuery(id+"F2.opPattern","COPY",BODY,{"derivedFrom":makeQuery(id+"F1.opRevolve","SWEPT_BODY",BODY,{"disambiguationData":[OSD([sQuery(id+"F0.wireOp",EDGE,"E1")])]}),"instanceName":"1"}),"instanceName":"1"}),"instanceName":"1"}),"instanceName":"1"}),"instanceName":"1"});
            var Q212;
            Q212=makeQuery(id+"F10.opPattern","COPY",BODY,{"derivedFrom":makeQuery(id+"F6.opPattern","COPY",BODY,{"derivedFrom":makeQuery(id+"F5.opPattern","COPY",BODY,{"derivedFrom":makeQuery(id+"F4.opPattern","COPY",BODY,{"derivedFrom":makeQuery(id+"F1.opRevolve","SWEPT_BODY",BODY,{"disambiguationData":[OSD([sQuery(id+"F0.wireOp",EDGE,"E1")])]}),"instanceName":"1"}),"instanceName":"1"}),"instanceName":"1"}),"instanceName":"1"});
            var Q213;
            Q213=makeQuery(id+"F10.opPattern","COPY",BODY,{"derivedFrom":makeQuery(id+"F6.opPattern","COPY",BODY,{"derivedFrom":makeQuery(id+"F5.opPattern","COPY",BODY,{"derivedFrom":makeQuery(id+"F4.opPattern","COPY",BODY,{"derivedFrom":makeQuery(id+"F2.opPattern","COPY",BODY,{"derivedFrom":makeQuery(id+"F1.opRevolve","SWEPT_BODY",BODY,{"disambiguationData":[OSD([sQuery(id+"F0.wireOp",EDGE,"E1")])]}),"instanceName":"1"}),"instanceName":"1"}),"instanceName":"1"}),"instanceName":"1"}),"instanceName":"1"});
            var Q214;
            Q214=makeQuery(id+"F10.opPattern","COPY",BODY,{"derivedFrom":makeQuery(id+"F6.opPattern","COPY",BODY,{"derivedFrom":makeQuery(id+"F5.opPattern","COPY",BODY,{"derivedFrom":makeQuery(id+"F4.opPattern","COPY",BODY,{"derivedFrom":makeQuery(id+"F3.opPattern","COPY",BODY,{"derivedFrom":makeQuery(id+"F2.opPattern","COPY",BODY,{"derivedFrom":makeQuery(id+"F1.opRevolve","SWEPT_BODY",BODY,{"disambiguationData":[OSD([sQuery(id+"F0.wireOp",EDGE,"E1")])]}),"instanceName":"1"}),"instanceName":"1"}),"instanceName":"1"}),"instanceName":"1"}),"instanceName":"1"}),"instanceName":"1"});
            var Q215;
            Q215=makeQuery(id+"F10.opPattern","COPY",BODY,{"derivedFrom":makeQuery(id+"F7.opPattern","COPY",BODY,{"derivedFrom":makeQuery(id+"F1.opRevolve","SWEPT_BODY",BODY,{"disambiguationData":[OSD([sQuery(id+"F0.wireOp",EDGE,"E1")])]}),"instanceName":"1"}),"instanceName":"1"});
            var Q216;
            Q216=makeQuery(id+"F10.opPattern","COPY",BODY,{"derivedFrom":makeQuery(id+"F7.opPattern","COPY",BODY,{"derivedFrom":makeQuery(id+"F2.opPattern","COPY",BODY,{"derivedFrom":makeQuery(id+"F1.opRevolve","SWEPT_BODY",BODY,{"disambiguationData":[OSD([sQuery(id+"F0.wireOp",EDGE,"E1")])]}),"instanceName":"1"}),"instanceName":"1"}),"instanceName":"1"});
            var Q217;
            Q217=makeQuery(id+"F10.opPattern","COPY",BODY,{"derivedFrom":makeQuery(id+"F7.opPattern","COPY",BODY,{"derivedFrom":makeQuery(id+"F3.opPattern","COPY",BODY,{"derivedFrom":makeQuery(id+"F2.opPattern","COPY",BODY,{"derivedFrom":makeQuery(id+"F1.opRevolve","SWEPT_BODY",BODY,{"disambiguationData":[OSD([sQuery(id+"F0.wireOp",EDGE,"E1")])]}),"instanceName":"1"}),"instanceName":"1"}),"instanceName":"1"}),"instanceName":"1"});
            var Q218;
            Q218=makeQuery(id+"F10.opPattern","COPY",BODY,{"derivedFrom":makeQuery(id+"F7.opPattern","COPY",BODY,{"derivedFrom":makeQuery(id+"F4.opPattern","COPY",BODY,{"derivedFrom":makeQuery(id+"F1.opRevolve","SWEPT_BODY",BODY,{"disambiguationData":[OSD([sQuery(id+"F0.wireOp",EDGE,"E1")])]}),"instanceName":"1"}),"instanceName":"1"}),"instanceName":"1"});
            var Q219;
            Q219=makeQuery(id+"F10.opPattern","COPY",BODY,{"derivedFrom":makeQuery(id+"F7.opPattern","COPY",BODY,{"derivedFrom":makeQuery(id+"F4.opPattern","COPY",BODY,{"derivedFrom":makeQuery(id+"F2.opPattern","COPY",BODY,{"derivedFrom":makeQuery(id+"F1.opRevolve","SWEPT_BODY",BODY,{"disambiguationData":[OSD([sQuery(id+"F0.wireOp",EDGE,"E1")])]}),"instanceName":"1"}),"instanceName":"1"}),"instanceName":"1"}),"instanceName":"1"});
            var Q220;
            Q220=makeQuery(id+"F10.opPattern","COPY",BODY,{"derivedFrom":makeQuery(id+"F7.opPattern","COPY",BODY,{"derivedFrom":makeQuery(id+"F4.opPattern","COPY",BODY,{"derivedFrom":makeQuery(id+"F3.opPattern","COPY",BODY,{"derivedFrom":makeQuery(id+"F2.opPattern","COPY",BODY,{"derivedFrom":makeQuery(id+"F1.opRevolve","SWEPT_BODY",BODY,{"disambiguationData":[OSD([sQuery(id+"F0.wireOp",EDGE,"E1")])]}),"instanceName":"1"}),"instanceName":"1"}),"instanceName":"1"}),"instanceName":"1"}),"instanceName":"1"});
            var Q221;
            Q221=makeQuery(id+"F10.opPattern","COPY",BODY,{"derivedFrom":makeQuery(id+"F7.opPattern","COPY",BODY,{"derivedFrom":makeQuery(id+"F5.opPattern","COPY",BODY,{"derivedFrom":makeQuery(id+"F1.opRevolve","SWEPT_BODY",BODY,{"disambiguationData":[OSD([sQuery(id+"F0.wireOp",EDGE,"E1")])]}),"instanceName":"1"}),"instanceName":"1"}),"instanceName":"1"});
            var Q222;
            Q222=makeQuery(id+"F10.opPattern","COPY",BODY,{"derivedFrom":makeQuery(id+"F7.opPattern","COPY",BODY,{"derivedFrom":makeQuery(id+"F5.opPattern","COPY",BODY,{"derivedFrom":makeQuery(id+"F2.opPattern","COPY",BODY,{"derivedFrom":makeQuery(id+"F1.opRevolve","SWEPT_BODY",BODY,{"disambiguationData":[OSD([sQuery(id+"F0.wireOp",EDGE,"E1")])]}),"instanceName":"1"}),"instanceName":"1"}),"instanceName":"1"}),"instanceName":"1"});
            var Q223;
            Q223=makeQuery(id+"F10.opPattern","COPY",BODY,{"derivedFrom":makeQuery(id+"F7.opPattern","COPY",BODY,{"derivedFrom":makeQuery(id+"F5.opPattern","COPY",BODY,{"derivedFrom":makeQuery(id+"F3.opPattern","COPY",BODY,{"derivedFrom":makeQuery(id+"F2.opPattern","COPY",BODY,{"derivedFrom":makeQuery(id+"F1.opRevolve","SWEPT_BODY",BODY,{"disambiguationData":[OSD([sQuery(id+"F0.wireOp",EDGE,"E1")])]}),"instanceName":"1"}),"instanceName":"1"}),"instanceName":"1"}),"instanceName":"1"}),"instanceName":"1"});
            var Q224;
            Q224=makeQuery(id+"F10.opPattern","COPY",BODY,{"derivedFrom":makeQuery(id+"F7.opPattern","COPY",BODY,{"derivedFrom":makeQuery(id+"F5.opPattern","COPY",BODY,{"derivedFrom":makeQuery(id+"F4.opPattern","COPY",BODY,{"derivedFrom":makeQuery(id+"F1.opRevolve","SWEPT_BODY",BODY,{"disambiguationData":[OSD([sQuery(id+"F0.wireOp",EDGE,"E1")])]}),"instanceName":"1"}),"instanceName":"1"}),"instanceName":"1"}),"instanceName":"1"});
            var Q225;
            Q225=makeQuery(id+"F10.opPattern","COPY",BODY,{"derivedFrom":makeQuery(id+"F7.opPattern","COPY",BODY,{"derivedFrom":makeQuery(id+"F5.opPattern","COPY",BODY,{"derivedFrom":makeQuery(id+"F4.opPattern","COPY",BODY,{"derivedFrom":makeQuery(id+"F2.opPattern","COPY",BODY,{"derivedFrom":makeQuery(id+"F1.opRevolve","SWEPT_BODY",BODY,{"disambiguationData":[OSD([sQuery(id+"F0.wireOp",EDGE,"E1")])]}),"instanceName":"1"}),"instanceName":"1"}),"instanceName":"1"}),"instanceName":"1"}),"instanceName":"1"});
            var Q226;
            Q226=makeQuery(id+"F10.opPattern","COPY",BODY,{"derivedFrom":makeQuery(id+"F7.opPattern","COPY",BODY,{"derivedFrom":makeQuery(id+"F5.opPattern","COPY",BODY,{"derivedFrom":makeQuery(id+"F4.opPattern","COPY",BODY,{"derivedFrom":makeQuery(id+"F3.opPattern","COPY",BODY,{"derivedFrom":makeQuery(id+"F2.opPattern","COPY",BODY,{"derivedFrom":makeQuery(id+"F1.opRevolve","SWEPT_BODY",BODY,{"disambiguationData":[OSD([sQuery(id+"F0.wireOp",EDGE,"E1")])]}),"instanceName":"1"}),"instanceName":"1"}),"instanceName":"1"}),"instanceName":"1"}),"instanceName":"1"}),"instanceName":"1"});
            var Q227;
            Q227=makeQuery(id+"F10.opPattern","COPY",BODY,{"derivedFrom":makeQuery(id+"F7.opPattern","COPY",BODY,{"derivedFrom":makeQuery(id+"F6.opPattern","COPY",BODY,{"derivedFrom":makeQuery(id+"F1.opRevolve","SWEPT_BODY",BODY,{"disambiguationData":[OSD([sQuery(id+"F0.wireOp",EDGE,"E1")])]}),"instanceName":"1"}),"instanceName":"1"}),"instanceName":"1"});
            var Q228;
            Q228=makeQuery(id+"F10.opPattern","COPY",BODY,{"derivedFrom":makeQuery(id+"F7.opPattern","COPY",BODY,{"derivedFrom":makeQuery(id+"F6.opPattern","COPY",BODY,{"derivedFrom":makeQuery(id+"F2.opPattern","COPY",BODY,{"derivedFrom":makeQuery(id+"F1.opRevolve","SWEPT_BODY",BODY,{"disambiguationData":[OSD([sQuery(id+"F0.wireOp",EDGE,"E1")])]}),"instanceName":"1"}),"instanceName":"1"}),"instanceName":"1"}),"instanceName":"1"});
            var Q229;
            Q229=makeQuery(id+"F10.opPattern","COPY",BODY,{"derivedFrom":makeQuery(id+"F7.opPattern","COPY",BODY,{"derivedFrom":makeQuery(id+"F6.opPattern","COPY",BODY,{"derivedFrom":makeQuery(id+"F3.opPattern","COPY",BODY,{"derivedFrom":makeQuery(id+"F2.opPattern","COPY",BODY,{"derivedFrom":makeQuery(id+"F1.opRevolve","SWEPT_BODY",BODY,{"disambiguationData":[OSD([sQuery(id+"F0.wireOp",EDGE,"E1")])]}),"instanceName":"1"}),"instanceName":"1"}),"instanceName":"1"}),"instanceName":"1"}),"instanceName":"1"});
            var Q230;
            Q230=makeQuery(id+"F10.opPattern","COPY",BODY,{"derivedFrom":makeQuery(id+"F7.opPattern","COPY",BODY,{"derivedFrom":makeQuery(id+"F6.opPattern","COPY",BODY,{"derivedFrom":makeQuery(id+"F4.opPattern","COPY",BODY,{"derivedFrom":makeQuery(id+"F1.opRevolve","SWEPT_BODY",BODY,{"disambiguationData":[OSD([sQuery(id+"F0.wireOp",EDGE,"E1")])]}),"instanceName":"1"}),"instanceName":"1"}),"instanceName":"1"}),"instanceName":"1"});
            var Q231;
            Q231=makeQuery(id+"F10.opPattern","COPY",BODY,{"derivedFrom":makeQuery(id+"F7.opPattern","COPY",BODY,{"derivedFrom":makeQuery(id+"F6.opPattern","COPY",BODY,{"derivedFrom":makeQuery(id+"F4.opPattern","COPY",BODY,{"derivedFrom":makeQuery(id+"F2.opPattern","COPY",BODY,{"derivedFrom":makeQuery(id+"F1.opRevolve","SWEPT_BODY",BODY,{"disambiguationData":[OSD([sQuery(id+"F0.wireOp",EDGE,"E1")])]}),"instanceName":"1"}),"instanceName":"1"}),"instanceName":"1"}),"instanceName":"1"}),"instanceName":"1"});
            var Q232;
            Q232=makeQuery(id+"F10.opPattern","COPY",BODY,{"derivedFrom":makeQuery(id+"F7.opPattern","COPY",BODY,{"derivedFrom":makeQuery(id+"F6.opPattern","COPY",BODY,{"derivedFrom":makeQuery(id+"F4.opPattern","COPY",BODY,{"derivedFrom":makeQuery(id+"F3.opPattern","COPY",BODY,{"derivedFrom":makeQuery(id+"F2.opPattern","COPY",BODY,{"derivedFrom":makeQuery(id+"F1.opRevolve","SWEPT_BODY",BODY,{"disambiguationData":[OSD([sQuery(id+"F0.wireOp",EDGE,"E1")])]}),"instanceName":"1"}),"instanceName":"1"}),"instanceName":"1"}),"instanceName":"1"}),"instanceName":"1"}),"instanceName":"1"});
            var Q233;
            Q233=makeQuery(id+"F10.opPattern","COPY",BODY,{"derivedFrom":makeQuery(id+"F7.opPattern","COPY",BODY,{"derivedFrom":makeQuery(id+"F6.opPattern","COPY",BODY,{"derivedFrom":makeQuery(id+"F5.opPattern","COPY",BODY,{"derivedFrom":makeQuery(id+"F1.opRevolve","SWEPT_BODY",BODY,{"disambiguationData":[OSD([sQuery(id+"F0.wireOp",EDGE,"E1")])]}),"instanceName":"1"}),"instanceName":"1"}),"instanceName":"1"}),"instanceName":"1"});
            var Q234;
            Q234=makeQuery(id+"F10.opPattern","COPY",BODY,{"derivedFrom":makeQuery(id+"F7.opPattern","COPY",BODY,{"derivedFrom":makeQuery(id+"F6.opPattern","COPY",BODY,{"derivedFrom":makeQuery(id+"F5.opPattern","COPY",BODY,{"derivedFrom":makeQuery(id+"F2.opPattern","COPY",BODY,{"derivedFrom":makeQuery(id+"F1.opRevolve","SWEPT_BODY",BODY,{"disambiguationData":[OSD([sQuery(id+"F0.wireOp",EDGE,"E1")])]}),"instanceName":"1"}),"instanceName":"1"}),"instanceName":"1"}),"instanceName":"1"}),"instanceName":"1"});
            var Q235;
            Q235=makeQuery(id+"F10.opPattern","COPY",BODY,{"derivedFrom":makeQuery(id+"F7.opPattern","COPY",BODY,{"derivedFrom":makeQuery(id+"F6.opPattern","COPY",BODY,{"derivedFrom":makeQuery(id+"F5.opPattern","COPY",BODY,{"derivedFrom":makeQuery(id+"F3.opPattern","COPY",BODY,{"derivedFrom":makeQuery(id+"F2.opPattern","COPY",BODY,{"derivedFrom":makeQuery(id+"F1.opRevolve","SWEPT_BODY",BODY,{"disambiguationData":[OSD([sQuery(id+"F0.wireOp",EDGE,"E1")])]}),"instanceName":"1"}),"instanceName":"1"}),"instanceName":"1"}),"instanceName":"1"}),"instanceName":"1"}),"instanceName":"1"});
            var Q236;
            Q236=makeQuery(id+"F10.opPattern","COPY",BODY,{"derivedFrom":makeQuery(id+"F7.opPattern","COPY",BODY,{"derivedFrom":makeQuery(id+"F6.opPattern","COPY",BODY,{"derivedFrom":makeQuery(id+"F5.opPattern","COPY",BODY,{"derivedFrom":makeQuery(id+"F4.opPattern","COPY",BODY,{"derivedFrom":makeQuery(id+"F1.opRevolve","SWEPT_BODY",BODY,{"disambiguationData":[OSD([sQuery(id+"F0.wireOp",EDGE,"E1")])]}),"instanceName":"1"}),"instanceName":"1"}),"instanceName":"1"}),"instanceName":"1"}),"instanceName":"1"});
            var Q237;
            Q237=makeQuery(id+"F10.opPattern","COPY",BODY,{"derivedFrom":makeQuery(id+"F7.opPattern","COPY",BODY,{"derivedFrom":makeQuery(id+"F6.opPattern","COPY",BODY,{"derivedFrom":makeQuery(id+"F5.opPattern","COPY",BODY,{"derivedFrom":makeQuery(id+"F4.opPattern","COPY",BODY,{"derivedFrom":makeQuery(id+"F2.opPattern","COPY",BODY,{"derivedFrom":makeQuery(id+"F1.opRevolve","SWEPT_BODY",BODY,{"disambiguationData":[OSD([sQuery(id+"F0.wireOp",EDGE,"E1")])]}),"instanceName":"1"}),"instanceName":"1"}),"instanceName":"1"}),"instanceName":"1"}),"instanceName":"1"}),"instanceName":"1"});
            var Q238;
            Q238=makeQuery(id+"F10.opPattern","COPY",BODY,{"derivedFrom":makeQuery(id+"F7.opPattern","COPY",BODY,{"derivedFrom":makeQuery(id+"F6.opPattern","COPY",BODY,{"derivedFrom":makeQuery(id+"F5.opPattern","COPY",BODY,{"derivedFrom":makeQuery(id+"F4.opPattern","COPY",BODY,{"derivedFrom":makeQuery(id+"F3.opPattern","COPY",BODY,{"derivedFrom":makeQuery(id+"F2.opPattern","COPY",BODY,{"derivedFrom":makeQuery(id+"F1.opRevolve","SWEPT_BODY",BODY,{"disambiguationData":[OSD([sQuery(id+"F0.wireOp",EDGE,"E1")])]}),"instanceName":"1"}),"instanceName":"1"}),"instanceName":"1"}),"instanceName":"1"}),"instanceName":"1"}),"instanceName":"1"}),"instanceName":"1"});
            var Q239;
            Q239=makeQuery(id+"F10.opPattern","COPY",BODY,{"derivedFrom":makeQuery(id+"F8.opPattern","COPY",BODY,{"derivedFrom":makeQuery(id+"F1.opRevolve","SWEPT_BODY",BODY,{"disambiguationData":[OSD([sQuery(id+"F0.wireOp",EDGE,"E1")])]}),"instanceName":"1"}),"instanceName":"1"});
            var Q240;
            Q240=makeQuery(id+"F10.opPattern","COPY",BODY,{"derivedFrom":makeQuery(id+"F8.opPattern","COPY",BODY,{"derivedFrom":makeQuery(id+"F2.opPattern","COPY",BODY,{"derivedFrom":makeQuery(id+"F1.opRevolve","SWEPT_BODY",BODY,{"disambiguationData":[OSD([sQuery(id+"F0.wireOp",EDGE,"E1")])]}),"instanceName":"1"}),"instanceName":"1"}),"instanceName":"1"});
            var Q241;
            Q241=makeQuery(id+"F10.opPattern","COPY",BODY,{"derivedFrom":makeQuery(id+"F8.opPattern","COPY",BODY,{"derivedFrom":makeQuery(id+"F3.opPattern","COPY",BODY,{"derivedFrom":makeQuery(id+"F2.opPattern","COPY",BODY,{"derivedFrom":makeQuery(id+"F1.opRevolve","SWEPT_BODY",BODY,{"disambiguationData":[OSD([sQuery(id+"F0.wireOp",EDGE,"E1")])]}),"instanceName":"1"}),"instanceName":"1"}),"instanceName":"1"}),"instanceName":"1"});
            var Q242;
            Q242=makeQuery(id+"F10.opPattern","COPY",BODY,{"derivedFrom":makeQuery(id+"F8.opPattern","COPY",BODY,{"derivedFrom":makeQuery(id+"F4.opPattern","COPY",BODY,{"derivedFrom":makeQuery(id+"F1.opRevolve","SWEPT_BODY",BODY,{"disambiguationData":[OSD([sQuery(id+"F0.wireOp",EDGE,"E1")])]}),"instanceName":"1"}),"instanceName":"1"}),"instanceName":"1"});
            var Q243;
            Q243=makeQuery(id+"F10.opPattern","COPY",BODY,{"derivedFrom":makeQuery(id+"F8.opPattern","COPY",BODY,{"derivedFrom":makeQuery(id+"F4.opPattern","COPY",BODY,{"derivedFrom":makeQuery(id+"F2.opPattern","COPY",BODY,{"derivedFrom":makeQuery(id+"F1.opRevolve","SWEPT_BODY",BODY,{"disambiguationData":[OSD([sQuery(id+"F0.wireOp",EDGE,"E1")])]}),"instanceName":"1"}),"instanceName":"1"}),"instanceName":"1"}),"instanceName":"1"});
            var Q244;
            Q244=makeQuery(id+"F10.opPattern","COPY",BODY,{"derivedFrom":makeQuery(id+"F8.opPattern","COPY",BODY,{"derivedFrom":makeQuery(id+"F4.opPattern","COPY",BODY,{"derivedFrom":makeQuery(id+"F3.opPattern","COPY",BODY,{"derivedFrom":makeQuery(id+"F2.opPattern","COPY",BODY,{"derivedFrom":makeQuery(id+"F1.opRevolve","SWEPT_BODY",BODY,{"disambiguationData":[OSD([sQuery(id+"F0.wireOp",EDGE,"E1")])]}),"instanceName":"1"}),"instanceName":"1"}),"instanceName":"1"}),"instanceName":"1"}),"instanceName":"1"});
            var Q245;
            Q245=makeQuery(id+"F10.opPattern","COPY",BODY,{"derivedFrom":makeQuery(id+"F8.opPattern","COPY",BODY,{"derivedFrom":makeQuery(id+"F5.opPattern","COPY",BODY,{"derivedFrom":makeQuery(id+"F1.opRevolve","SWEPT_BODY",BODY,{"disambiguationData":[OSD([sQuery(id+"F0.wireOp",EDGE,"E1")])]}),"instanceName":"1"}),"instanceName":"1"}),"instanceName":"1"});
            var Q246;
            Q246=makeQuery(id+"F10.opPattern","COPY",BODY,{"derivedFrom":makeQuery(id+"F8.opPattern","COPY",BODY,{"derivedFrom":makeQuery(id+"F5.opPattern","COPY",BODY,{"derivedFrom":makeQuery(id+"F2.opPattern","COPY",BODY,{"derivedFrom":makeQuery(id+"F1.opRevolve","SWEPT_BODY",BODY,{"disambiguationData":[OSD([sQuery(id+"F0.wireOp",EDGE,"E1")])]}),"instanceName":"1"}),"instanceName":"1"}),"instanceName":"1"}),"instanceName":"1"});
            var Q247;
            Q247=makeQuery(id+"F10.opPattern","COPY",BODY,{"derivedFrom":makeQuery(id+"F8.opPattern","COPY",BODY,{"derivedFrom":makeQuery(id+"F5.opPattern","COPY",BODY,{"derivedFrom":makeQuery(id+"F3.opPattern","COPY",BODY,{"derivedFrom":makeQuery(id+"F2.opPattern","COPY",BODY,{"derivedFrom":makeQuery(id+"F1.opRevolve","SWEPT_BODY",BODY,{"disambiguationData":[OSD([sQuery(id+"F0.wireOp",EDGE,"E1")])]}),"instanceName":"1"}),"instanceName":"1"}),"instanceName":"1"}),"instanceName":"1"}),"instanceName":"1"});
            var Q248;
            Q248=makeQuery(id+"F10.opPattern","COPY",BODY,{"derivedFrom":makeQuery(id+"F8.opPattern","COPY",BODY,{"derivedFrom":makeQuery(id+"F5.opPattern","COPY",BODY,{"derivedFrom":makeQuery(id+"F4.opPattern","COPY",BODY,{"derivedFrom":makeQuery(id+"F1.opRevolve","SWEPT_BODY",BODY,{"disambiguationData":[OSD([sQuery(id+"F0.wireOp",EDGE,"E1")])]}),"instanceName":"1"}),"instanceName":"1"}),"instanceName":"1"}),"instanceName":"1"});
            var Q249;
            Q249=makeQuery(id+"F10.opPattern","COPY",BODY,{"derivedFrom":makeQuery(id+"F8.opPattern","COPY",BODY,{"derivedFrom":makeQuery(id+"F5.opPattern","COPY",BODY,{"derivedFrom":makeQuery(id+"F4.opPattern","COPY",BODY,{"derivedFrom":makeQuery(id+"F2.opPattern","COPY",BODY,{"derivedFrom":makeQuery(id+"F1.opRevolve","SWEPT_BODY",BODY,{"disambiguationData":[OSD([sQuery(id+"F0.wireOp",EDGE,"E1")])]}),"instanceName":"1"}),"instanceName":"1"}),"instanceName":"1"}),"instanceName":"1"}),"instanceName":"1"});
            var Q250;
            Q250=makeQuery(id+"F10.opPattern","COPY",BODY,{"derivedFrom":makeQuery(id+"F8.opPattern","COPY",BODY,{"derivedFrom":makeQuery(id+"F5.opPattern","COPY",BODY,{"derivedFrom":makeQuery(id+"F4.opPattern","COPY",BODY,{"derivedFrom":makeQuery(id+"F3.opPattern","COPY",BODY,{"derivedFrom":makeQuery(id+"F2.opPattern","COPY",BODY,{"derivedFrom":makeQuery(id+"F1.opRevolve","SWEPT_BODY",BODY,{"disambiguationData":[OSD([sQuery(id+"F0.wireOp",EDGE,"E1")])]}),"instanceName":"1"}),"instanceName":"1"}),"instanceName":"1"}),"instanceName":"1"}),"instanceName":"1"}),"instanceName":"1"});
            var Q251;
            Q251=makeQuery(id+"F10.opPattern","COPY",BODY,{"derivedFrom":makeQuery(id+"F8.opPattern","COPY",BODY,{"derivedFrom":makeQuery(id+"F6.opPattern","COPY",BODY,{"derivedFrom":makeQuery(id+"F1.opRevolve","SWEPT_BODY",BODY,{"disambiguationData":[OSD([sQuery(id+"F0.wireOp",EDGE,"E1")])]}),"instanceName":"1"}),"instanceName":"1"}),"instanceName":"1"});
            var Q252;
            Q252=makeQuery(id+"F10.opPattern","COPY",BODY,{"derivedFrom":makeQuery(id+"F8.opPattern","COPY",BODY,{"derivedFrom":makeQuery(id+"F6.opPattern","COPY",BODY,{"derivedFrom":makeQuery(id+"F2.opPattern","COPY",BODY,{"derivedFrom":makeQuery(id+"F1.opRevolve","SWEPT_BODY",BODY,{"disambiguationData":[OSD([sQuery(id+"F0.wireOp",EDGE,"E1")])]}),"instanceName":"1"}),"instanceName":"1"}),"instanceName":"1"}),"instanceName":"1"});
            var Q253;
            Q253=makeQuery(id+"F10.opPattern","COPY",BODY,{"derivedFrom":makeQuery(id+"F8.opPattern","COPY",BODY,{"derivedFrom":makeQuery(id+"F6.opPattern","COPY",BODY,{"derivedFrom":makeQuery(id+"F3.opPattern","COPY",BODY,{"derivedFrom":makeQuery(id+"F2.opPattern","COPY",BODY,{"derivedFrom":makeQuery(id+"F1.opRevolve","SWEPT_BODY",BODY,{"disambiguationData":[OSD([sQuery(id+"F0.wireOp",EDGE,"E1")])]}),"instanceName":"1"}),"instanceName":"1"}),"instanceName":"1"}),"instanceName":"1"}),"instanceName":"1"});
            var Q254;
            Q254=makeQuery(id+"F10.opPattern","COPY",BODY,{"derivedFrom":makeQuery(id+"F8.opPattern","COPY",BODY,{"derivedFrom":makeQuery(id+"F6.opPattern","COPY",BODY,{"derivedFrom":makeQuery(id+"F4.opPattern","COPY",BODY,{"derivedFrom":makeQuery(id+"F1.opRevolve","SWEPT_BODY",BODY,{"disambiguationData":[OSD([sQuery(id+"F0.wireOp",EDGE,"E1")])]}),"instanceName":"1"}),"instanceName":"1"}),"instanceName":"1"}),"instanceName":"1"});
            var Q255;
            Q255=makeQuery(id+"F10.opPattern","COPY",BODY,{"derivedFrom":makeQuery(id+"F8.opPattern","COPY",BODY,{"derivedFrom":makeQuery(id+"F6.opPattern","COPY",BODY,{"derivedFrom":makeQuery(id+"F4.opPattern","COPY",BODY,{"derivedFrom":makeQuery(id+"F2.opPattern","COPY",BODY,{"derivedFrom":makeQuery(id+"F1.opRevolve","SWEPT_BODY",BODY,{"disambiguationData":[OSD([sQuery(id+"F0.wireOp",EDGE,"E1")])]}),"instanceName":"1"}),"instanceName":"1"}),"instanceName":"1"}),"instanceName":"1"}),"instanceName":"1"});
            var Q256;
            Q256=makeQuery(id+"F10.opPattern","COPY",BODY,{"derivedFrom":makeQuery(id+"F8.opPattern","COPY",BODY,{"derivedFrom":makeQuery(id+"F6.opPattern","COPY",BODY,{"derivedFrom":makeQuery(id+"F4.opPattern","COPY",BODY,{"derivedFrom":makeQuery(id+"F3.opPattern","COPY",BODY,{"derivedFrom":makeQuery(id+"F2.opPattern","COPY",BODY,{"derivedFrom":makeQuery(id+"F1.opRevolve","SWEPT_BODY",BODY,{"disambiguationData":[OSD([sQuery(id+"F0.wireOp",EDGE,"E1")])]}),"instanceName":"1"}),"instanceName":"1"}),"instanceName":"1"}),"instanceName":"1"}),"instanceName":"1"}),"instanceName":"1"});
            var Q257;
            Q257=makeQuery(id+"F10.opPattern","COPY",BODY,{"derivedFrom":makeQuery(id+"F8.opPattern","COPY",BODY,{"derivedFrom":makeQuery(id+"F6.opPattern","COPY",BODY,{"derivedFrom":makeQuery(id+"F5.opPattern","COPY",BODY,{"derivedFrom":makeQuery(id+"F1.opRevolve","SWEPT_BODY",BODY,{"disambiguationData":[OSD([sQuery(id+"F0.wireOp",EDGE,"E1")])]}),"instanceName":"1"}),"instanceName":"1"}),"instanceName":"1"}),"instanceName":"1"});
            var Q258;
            Q258=makeQuery(id+"F10.opPattern","COPY",BODY,{"derivedFrom":makeQuery(id+"F8.opPattern","COPY",BODY,{"derivedFrom":makeQuery(id+"F6.opPattern","COPY",BODY,{"derivedFrom":makeQuery(id+"F5.opPattern","COPY",BODY,{"derivedFrom":makeQuery(id+"F2.opPattern","COPY",BODY,{"derivedFrom":makeQuery(id+"F1.opRevolve","SWEPT_BODY",BODY,{"disambiguationData":[OSD([sQuery(id+"F0.wireOp",EDGE,"E1")])]}),"instanceName":"1"}),"instanceName":"1"}),"instanceName":"1"}),"instanceName":"1"}),"instanceName":"1"});
            var Q259;
            Q259=makeQuery(id+"F10.opPattern","COPY",BODY,{"derivedFrom":makeQuery(id+"F8.opPattern","COPY",BODY,{"derivedFrom":makeQuery(id+"F6.opPattern","COPY",BODY,{"derivedFrom":makeQuery(id+"F5.opPattern","COPY",BODY,{"derivedFrom":makeQuery(id+"F3.opPattern","COPY",BODY,{"derivedFrom":makeQuery(id+"F2.opPattern","COPY",BODY,{"derivedFrom":makeQuery(id+"F1.opRevolve","SWEPT_BODY",BODY,{"disambiguationData":[OSD([sQuery(id+"F0.wireOp",EDGE,"E1")])]}),"instanceName":"1"}),"instanceName":"1"}),"instanceName":"1"}),"instanceName":"1"}),"instanceName":"1"}),"instanceName":"1"});
            var Q260;
            Q260=makeQuery(id+"F10.opPattern","COPY",BODY,{"derivedFrom":makeQuery(id+"F8.opPattern","COPY",BODY,{"derivedFrom":makeQuery(id+"F6.opPattern","COPY",BODY,{"derivedFrom":makeQuery(id+"F5.opPattern","COPY",BODY,{"derivedFrom":makeQuery(id+"F4.opPattern","COPY",BODY,{"derivedFrom":makeQuery(id+"F1.opRevolve","SWEPT_BODY",BODY,{"disambiguationData":[OSD([sQuery(id+"F0.wireOp",EDGE,"E1")])]}),"instanceName":"1"}),"instanceName":"1"}),"instanceName":"1"}),"instanceName":"1"}),"instanceName":"1"});
            var Q261;
            Q261=makeQuery(id+"F10.opPattern","COPY",BODY,{"derivedFrom":makeQuery(id+"F8.opPattern","COPY",BODY,{"derivedFrom":makeQuery(id+"F6.opPattern","COPY",BODY,{"derivedFrom":makeQuery(id+"F5.opPattern","COPY",BODY,{"derivedFrom":makeQuery(id+"F4.opPattern","COPY",BODY,{"derivedFrom":makeQuery(id+"F2.opPattern","COPY",BODY,{"derivedFrom":makeQuery(id+"F1.opRevolve","SWEPT_BODY",BODY,{"disambiguationData":[OSD([sQuery(id+"F0.wireOp",EDGE,"E1")])]}),"instanceName":"1"}),"instanceName":"1"}),"instanceName":"1"}),"instanceName":"1"}),"instanceName":"1"}),"instanceName":"1"});
            var Q262;
            Q262=makeQuery(id+"F10.opPattern","COPY",BODY,{"derivedFrom":makeQuery(id+"F8.opPattern","COPY",BODY,{"derivedFrom":makeQuery(id+"F6.opPattern","COPY",BODY,{"derivedFrom":makeQuery(id+"F5.opPattern","COPY",BODY,{"derivedFrom":makeQuery(id+"F4.opPattern","COPY",BODY,{"derivedFrom":makeQuery(id+"F3.opPattern","COPY",BODY,{"derivedFrom":makeQuery(id+"F2.opPattern","COPY",BODY,{"derivedFrom":makeQuery(id+"F1.opRevolve","SWEPT_BODY",BODY,{"disambiguationData":[OSD([sQuery(id+"F0.wireOp",EDGE,"E1")])]}),"instanceName":"1"}),"instanceName":"1"}),"instanceName":"1"}),"instanceName":"1"}),"instanceName":"1"}),"instanceName":"1"}),"instanceName":"1"});
            var Q263;
            Q263=makeQuery(id+"F10.opPattern","COPY",BODY,{"derivedFrom":makeQuery(id+"F8.opPattern","COPY",BODY,{"derivedFrom":makeQuery(id+"F7.opPattern","COPY",BODY,{"derivedFrom":makeQuery(id+"F1.opRevolve","SWEPT_BODY",BODY,{"disambiguationData":[OSD([sQuery(id+"F0.wireOp",EDGE,"E1")])]}),"instanceName":"1"}),"instanceName":"1"}),"instanceName":"1"});
            var Q264;
            Q264=makeQuery(id+"F10.opPattern","COPY",BODY,{"derivedFrom":makeQuery(id+"F8.opPattern","COPY",BODY,{"derivedFrom":makeQuery(id+"F7.opPattern","COPY",BODY,{"derivedFrom":makeQuery(id+"F2.opPattern","COPY",BODY,{"derivedFrom":makeQuery(id+"F1.opRevolve","SWEPT_BODY",BODY,{"disambiguationData":[OSD([sQuery(id+"F0.wireOp",EDGE,"E1")])]}),"instanceName":"1"}),"instanceName":"1"}),"instanceName":"1"}),"instanceName":"1"});
            var Q265;
            Q265=makeQuery(id+"F10.opPattern","COPY",BODY,{"derivedFrom":makeQuery(id+"F8.opPattern","COPY",BODY,{"derivedFrom":makeQuery(id+"F7.opPattern","COPY",BODY,{"derivedFrom":makeQuery(id+"F3.opPattern","COPY",BODY,{"derivedFrom":makeQuery(id+"F2.opPattern","COPY",BODY,{"derivedFrom":makeQuery(id+"F1.opRevolve","SWEPT_BODY",BODY,{"disambiguationData":[OSD([sQuery(id+"F0.wireOp",EDGE,"E1")])]}),"instanceName":"1"}),"instanceName":"1"}),"instanceName":"1"}),"instanceName":"1"}),"instanceName":"1"});
            var Q266;
            Q266=makeQuery(id+"F10.opPattern","COPY",BODY,{"derivedFrom":makeQuery(id+"F8.opPattern","COPY",BODY,{"derivedFrom":makeQuery(id+"F7.opPattern","COPY",BODY,{"derivedFrom":makeQuery(id+"F4.opPattern","COPY",BODY,{"derivedFrom":makeQuery(id+"F1.opRevolve","SWEPT_BODY",BODY,{"disambiguationData":[OSD([sQuery(id+"F0.wireOp",EDGE,"E1")])]}),"instanceName":"1"}),"instanceName":"1"}),"instanceName":"1"}),"instanceName":"1"});
            var Q267;
            Q267=makeQuery(id+"F10.opPattern","COPY",BODY,{"derivedFrom":makeQuery(id+"F8.opPattern","COPY",BODY,{"derivedFrom":makeQuery(id+"F7.opPattern","COPY",BODY,{"derivedFrom":makeQuery(id+"F4.opPattern","COPY",BODY,{"derivedFrom":makeQuery(id+"F2.opPattern","COPY",BODY,{"derivedFrom":makeQuery(id+"F1.opRevolve","SWEPT_BODY",BODY,{"disambiguationData":[OSD([sQuery(id+"F0.wireOp",EDGE,"E1")])]}),"instanceName":"1"}),"instanceName":"1"}),"instanceName":"1"}),"instanceName":"1"}),"instanceName":"1"});
            var Q268;
            Q268=makeQuery(id+"F10.opPattern","COPY",BODY,{"derivedFrom":makeQuery(id+"F8.opPattern","COPY",BODY,{"derivedFrom":makeQuery(id+"F7.opPattern","COPY",BODY,{"derivedFrom":makeQuery(id+"F4.opPattern","COPY",BODY,{"derivedFrom":makeQuery(id+"F3.opPattern","COPY",BODY,{"derivedFrom":makeQuery(id+"F2.opPattern","COPY",BODY,{"derivedFrom":makeQuery(id+"F1.opRevolve","SWEPT_BODY",BODY,{"disambiguationData":[OSD([sQuery(id+"F0.wireOp",EDGE,"E1")])]}),"instanceName":"1"}),"instanceName":"1"}),"instanceName":"1"}),"instanceName":"1"}),"instanceName":"1"}),"instanceName":"1"});
            var Q269;
            Q269=makeQuery(id+"F10.opPattern","COPY",BODY,{"derivedFrom":makeQuery(id+"F8.opPattern","COPY",BODY,{"derivedFrom":makeQuery(id+"F7.opPattern","COPY",BODY,{"derivedFrom":makeQuery(id+"F5.opPattern","COPY",BODY,{"derivedFrom":makeQuery(id+"F1.opRevolve","SWEPT_BODY",BODY,{"disambiguationData":[OSD([sQuery(id+"F0.wireOp",EDGE,"E1")])]}),"instanceName":"1"}),"instanceName":"1"}),"instanceName":"1"}),"instanceName":"1"});
            var Q270;
            Q270=makeQuery(id+"F10.opPattern","COPY",BODY,{"derivedFrom":makeQuery(id+"F8.opPattern","COPY",BODY,{"derivedFrom":makeQuery(id+"F7.opPattern","COPY",BODY,{"derivedFrom":makeQuery(id+"F5.opPattern","COPY",BODY,{"derivedFrom":makeQuery(id+"F2.opPattern","COPY",BODY,{"derivedFrom":makeQuery(id+"F1.opRevolve","SWEPT_BODY",BODY,{"disambiguationData":[OSD([sQuery(id+"F0.wireOp",EDGE,"E1")])]}),"instanceName":"1"}),"instanceName":"1"}),"instanceName":"1"}),"instanceName":"1"}),"instanceName":"1"});
            var Q271;
            Q271=makeQuery(id+"F10.opPattern","COPY",BODY,{"derivedFrom":makeQuery(id+"F8.opPattern","COPY",BODY,{"derivedFrom":makeQuery(id+"F7.opPattern","COPY",BODY,{"derivedFrom":makeQuery(id+"F5.opPattern","COPY",BODY,{"derivedFrom":makeQuery(id+"F3.opPattern","COPY",BODY,{"derivedFrom":makeQuery(id+"F2.opPattern","COPY",BODY,{"derivedFrom":makeQuery(id+"F1.opRevolve","SWEPT_BODY",BODY,{"disambiguationData":[OSD([sQuery(id+"F0.wireOp",EDGE,"E1")])]}),"instanceName":"1"}),"instanceName":"1"}),"instanceName":"1"}),"instanceName":"1"}),"instanceName":"1"}),"instanceName":"1"});
            var Q272;
            Q272=makeQuery(id+"F10.opPattern","COPY",BODY,{"derivedFrom":makeQuery(id+"F8.opPattern","COPY",BODY,{"derivedFrom":makeQuery(id+"F7.opPattern","COPY",BODY,{"derivedFrom":makeQuery(id+"F5.opPattern","COPY",BODY,{"derivedFrom":makeQuery(id+"F4.opPattern","COPY",BODY,{"derivedFrom":makeQuery(id+"F1.opRevolve","SWEPT_BODY",BODY,{"disambiguationData":[OSD([sQuery(id+"F0.wireOp",EDGE,"E1")])]}),"instanceName":"1"}),"instanceName":"1"}),"instanceName":"1"}),"instanceName":"1"}),"instanceName":"1"});
            var Q273;
            Q273=makeQuery(id+"F10.opPattern","COPY",BODY,{"derivedFrom":makeQuery(id+"F8.opPattern","COPY",BODY,{"derivedFrom":makeQuery(id+"F7.opPattern","COPY",BODY,{"derivedFrom":makeQuery(id+"F5.opPattern","COPY",BODY,{"derivedFrom":makeQuery(id+"F4.opPattern","COPY",BODY,{"derivedFrom":makeQuery(id+"F2.opPattern","COPY",BODY,{"derivedFrom":makeQuery(id+"F1.opRevolve","SWEPT_BODY",BODY,{"disambiguationData":[OSD([sQuery(id+"F0.wireOp",EDGE,"E1")])]}),"instanceName":"1"}),"instanceName":"1"}),"instanceName":"1"}),"instanceName":"1"}),"instanceName":"1"}),"instanceName":"1"});
            var Q274;
            Q274=makeQuery(id+"F10.opPattern","COPY",BODY,{"derivedFrom":makeQuery(id+"F8.opPattern","COPY",BODY,{"derivedFrom":makeQuery(id+"F7.opPattern","COPY",BODY,{"derivedFrom":makeQuery(id+"F5.opPattern","COPY",BODY,{"derivedFrom":makeQuery(id+"F4.opPattern","COPY",BODY,{"derivedFrom":makeQuery(id+"F3.opPattern","COPY",BODY,{"derivedFrom":makeQuery(id+"F2.opPattern","COPY",BODY,{"derivedFrom":makeQuery(id+"F1.opRevolve","SWEPT_BODY",BODY,{"disambiguationData":[OSD([sQuery(id+"F0.wireOp",EDGE,"E1")])]}),"instanceName":"1"}),"instanceName":"1"}),"instanceName":"1"}),"instanceName":"1"}),"instanceName":"1"}),"instanceName":"1"}),"instanceName":"1"});
            var Q275;
            Q275=makeQuery(id+"F10.opPattern","COPY",BODY,{"derivedFrom":makeQuery(id+"F8.opPattern","COPY",BODY,{"derivedFrom":makeQuery(id+"F7.opPattern","COPY",BODY,{"derivedFrom":makeQuery(id+"F6.opPattern","COPY",BODY,{"derivedFrom":makeQuery(id+"F1.opRevolve","SWEPT_BODY",BODY,{"disambiguationData":[OSD([sQuery(id+"F0.wireOp",EDGE,"E1")])]}),"instanceName":"1"}),"instanceName":"1"}),"instanceName":"1"}),"instanceName":"1"});
            var Q276;
            Q276=makeQuery(id+"F10.opPattern","COPY",BODY,{"derivedFrom":makeQuery(id+"F8.opPattern","COPY",BODY,{"derivedFrom":makeQuery(id+"F7.opPattern","COPY",BODY,{"derivedFrom":makeQuery(id+"F6.opPattern","COPY",BODY,{"derivedFrom":makeQuery(id+"F2.opPattern","COPY",BODY,{"derivedFrom":makeQuery(id+"F1.opRevolve","SWEPT_BODY",BODY,{"disambiguationData":[OSD([sQuery(id+"F0.wireOp",EDGE,"E1")])]}),"instanceName":"1"}),"instanceName":"1"}),"instanceName":"1"}),"instanceName":"1"}),"instanceName":"1"});
            var Q277;
            Q277=makeQuery(id+"F10.opPattern","COPY",BODY,{"derivedFrom":makeQuery(id+"F8.opPattern","COPY",BODY,{"derivedFrom":makeQuery(id+"F7.opPattern","COPY",BODY,{"derivedFrom":makeQuery(id+"F6.opPattern","COPY",BODY,{"derivedFrom":makeQuery(id+"F3.opPattern","COPY",BODY,{"derivedFrom":makeQuery(id+"F2.opPattern","COPY",BODY,{"derivedFrom":makeQuery(id+"F1.opRevolve","SWEPT_BODY",BODY,{"disambiguationData":[OSD([sQuery(id+"F0.wireOp",EDGE,"E1")])]}),"instanceName":"1"}),"instanceName":"1"}),"instanceName":"1"}),"instanceName":"1"}),"instanceName":"1"}),"instanceName":"1"});
            var Q278;
            Q278=makeQuery(id+"F10.opPattern","COPY",BODY,{"derivedFrom":makeQuery(id+"F8.opPattern","COPY",BODY,{"derivedFrom":makeQuery(id+"F7.opPattern","COPY",BODY,{"derivedFrom":makeQuery(id+"F6.opPattern","COPY",BODY,{"derivedFrom":makeQuery(id+"F4.opPattern","COPY",BODY,{"derivedFrom":makeQuery(id+"F1.opRevolve","SWEPT_BODY",BODY,{"disambiguationData":[OSD([sQuery(id+"F0.wireOp",EDGE,"E1")])]}),"instanceName":"1"}),"instanceName":"1"}),"instanceName":"1"}),"instanceName":"1"}),"instanceName":"1"});
            var Q279;
            Q279=makeQuery(id+"F10.opPattern","COPY",BODY,{"derivedFrom":makeQuery(id+"F8.opPattern","COPY",BODY,{"derivedFrom":makeQuery(id+"F7.opPattern","COPY",BODY,{"derivedFrom":makeQuery(id+"F6.opPattern","COPY",BODY,{"derivedFrom":makeQuery(id+"F4.opPattern","COPY",BODY,{"derivedFrom":makeQuery(id+"F2.opPattern","COPY",BODY,{"derivedFrom":makeQuery(id+"F1.opRevolve","SWEPT_BODY",BODY,{"disambiguationData":[OSD([sQuery(id+"F0.wireOp",EDGE,"E1")])]}),"instanceName":"1"}),"instanceName":"1"}),"instanceName":"1"}),"instanceName":"1"}),"instanceName":"1"}),"instanceName":"1"});
            var Q280;
            Q280=makeQuery(id+"F10.opPattern","COPY",BODY,{"derivedFrom":makeQuery(id+"F8.opPattern","COPY",BODY,{"derivedFrom":makeQuery(id+"F7.opPattern","COPY",BODY,{"derivedFrom":makeQuery(id+"F6.opPattern","COPY",BODY,{"derivedFrom":makeQuery(id+"F4.opPattern","COPY",BODY,{"derivedFrom":makeQuery(id+"F3.opPattern","COPY",BODY,{"derivedFrom":makeQuery(id+"F2.opPattern","COPY",BODY,{"derivedFrom":makeQuery(id+"F1.opRevolve","SWEPT_BODY",BODY,{"disambiguationData":[OSD([sQuery(id+"F0.wireOp",EDGE,"E1")])]}),"instanceName":"1"}),"instanceName":"1"}),"instanceName":"1"}),"instanceName":"1"}),"instanceName":"1"}),"instanceName":"1"}),"instanceName":"1"});
            var Q281;
            Q281=makeQuery(id+"F10.opPattern","COPY",BODY,{"derivedFrom":makeQuery(id+"F8.opPattern","COPY",BODY,{"derivedFrom":makeQuery(id+"F7.opPattern","COPY",BODY,{"derivedFrom":makeQuery(id+"F6.opPattern","COPY",BODY,{"derivedFrom":makeQuery(id+"F5.opPattern","COPY",BODY,{"derivedFrom":makeQuery(id+"F1.opRevolve","SWEPT_BODY",BODY,{"disambiguationData":[OSD([sQuery(id+"F0.wireOp",EDGE,"E1")])]}),"instanceName":"1"}),"instanceName":"1"}),"instanceName":"1"}),"instanceName":"1"}),"instanceName":"1"});
            var Q282;
            Q282=makeQuery(id+"F10.opPattern","COPY",BODY,{"derivedFrom":makeQuery(id+"F8.opPattern","COPY",BODY,{"derivedFrom":makeQuery(id+"F7.opPattern","COPY",BODY,{"derivedFrom":makeQuery(id+"F6.opPattern","COPY",BODY,{"derivedFrom":makeQuery(id+"F5.opPattern","COPY",BODY,{"derivedFrom":makeQuery(id+"F2.opPattern","COPY",BODY,{"derivedFrom":makeQuery(id+"F1.opRevolve","SWEPT_BODY",BODY,{"disambiguationData":[OSD([sQuery(id+"F0.wireOp",EDGE,"E1")])]}),"instanceName":"1"}),"instanceName":"1"}),"instanceName":"1"}),"instanceName":"1"}),"instanceName":"1"}),"instanceName":"1"});
            var Q283;
            Q283=makeQuery(id+"F10.opPattern","COPY",BODY,{"derivedFrom":makeQuery(id+"F8.opPattern","COPY",BODY,{"derivedFrom":makeQuery(id+"F7.opPattern","COPY",BODY,{"derivedFrom":makeQuery(id+"F6.opPattern","COPY",BODY,{"derivedFrom":makeQuery(id+"F5.opPattern","COPY",BODY,{"derivedFrom":makeQuery(id+"F3.opPattern","COPY",BODY,{"derivedFrom":makeQuery(id+"F2.opPattern","COPY",BODY,{"derivedFrom":makeQuery(id+"F1.opRevolve","SWEPT_BODY",BODY,{"disambiguationData":[OSD([sQuery(id+"F0.wireOp",EDGE,"E1")])]}),"instanceName":"1"}),"instanceName":"1"}),"instanceName":"1"}),"instanceName":"1"}),"instanceName":"1"}),"instanceName":"1"}),"instanceName":"1"});
            var Q284;
            Q284=makeQuery(id+"F10.opPattern","COPY",BODY,{"derivedFrom":makeQuery(id+"F8.opPattern","COPY",BODY,{"derivedFrom":makeQuery(id+"F7.opPattern","COPY",BODY,{"derivedFrom":makeQuery(id+"F6.opPattern","COPY",BODY,{"derivedFrom":makeQuery(id+"F5.opPattern","COPY",BODY,{"derivedFrom":makeQuery(id+"F4.opPattern","COPY",BODY,{"derivedFrom":makeQuery(id+"F1.opRevolve","SWEPT_BODY",BODY,{"disambiguationData":[OSD([sQuery(id+"F0.wireOp",EDGE,"E1")])]}),"instanceName":"1"}),"instanceName":"1"}),"instanceName":"1"}),"instanceName":"1"}),"instanceName":"1"}),"instanceName":"1"});
            var Q285;
            Q285=makeQuery(id+"F10.opPattern","COPY",BODY,{"derivedFrom":makeQuery(id+"F8.opPattern","COPY",BODY,{"derivedFrom":makeQuery(id+"F7.opPattern","COPY",BODY,{"derivedFrom":makeQuery(id+"F6.opPattern","COPY",BODY,{"derivedFrom":makeQuery(id+"F5.opPattern","COPY",BODY,{"derivedFrom":makeQuery(id+"F4.opPattern","COPY",BODY,{"derivedFrom":makeQuery(id+"F2.opPattern","COPY",BODY,{"derivedFrom":makeQuery(id+"F1.opRevolve","SWEPT_BODY",BODY,{"disambiguationData":[OSD([sQuery(id+"F0.wireOp",EDGE,"E1")])]}),"instanceName":"1"}),"instanceName":"1"}),"instanceName":"1"}),"instanceName":"1"}),"instanceName":"1"}),"instanceName":"1"}),"instanceName":"1"});
            var Q286;
            Q286=makeQuery(id+"F10.opPattern","COPY",BODY,{"derivedFrom":makeQuery(id+"F8.opPattern","COPY",BODY,{"derivedFrom":makeQuery(id+"F7.opPattern","COPY",BODY,{"derivedFrom":makeQuery(id+"F6.opPattern","COPY",BODY,{"derivedFrom":makeQuery(id+"F5.opPattern","COPY",BODY,{"derivedFrom":makeQuery(id+"F4.opPattern","COPY",BODY,{"derivedFrom":makeQuery(id+"F3.opPattern","COPY",BODY,{"derivedFrom":makeQuery(id+"F2.opPattern","COPY",BODY,{"derivedFrom":makeQuery(id+"F1.opRevolve","SWEPT_BODY",BODY,{"disambiguationData":[OSD([sQuery(id+"F0.wireOp",EDGE,"E1")])]}),"instanceName":"1"}),"instanceName":"1"}),"instanceName":"1"}),"instanceName":"1"}),"instanceName":"1"}),"instanceName":"1"}),"instanceName":"1"}),"instanceName":"1"});
            var Q287;
            Q287=makeQuery(id+"F10.opPattern","COPY",BODY,{"derivedFrom":makeQuery(id+"F9.opPattern","COPY",BODY,{"derivedFrom":makeQuery(id+"F1.opRevolve","SWEPT_BODY",BODY,{"disambiguationData":[OSD([sQuery(id+"F0.wireOp",EDGE,"E1")])]}),"instanceName":"1"}),"instanceName":"1"});
            var Q288;
            Q288=makeQuery(id+"F10.opPattern","COPY",BODY,{"derivedFrom":makeQuery(id+"F9.opPattern","COPY",BODY,{"derivedFrom":makeQuery(id+"F2.opPattern","COPY",BODY,{"derivedFrom":makeQuery(id+"F1.opRevolve","SWEPT_BODY",BODY,{"disambiguationData":[OSD([sQuery(id+"F0.wireOp",EDGE,"E1")])]}),"instanceName":"1"}),"instanceName":"1"}),"instanceName":"1"});
            var Q289;
            Q289=makeQuery(id+"F10.opPattern","COPY",BODY,{"derivedFrom":makeQuery(id+"F9.opPattern","COPY",BODY,{"derivedFrom":makeQuery(id+"F3.opPattern","COPY",BODY,{"derivedFrom":makeQuery(id+"F2.opPattern","COPY",BODY,{"derivedFrom":makeQuery(id+"F1.opRevolve","SWEPT_BODY",BODY,{"disambiguationData":[OSD([sQuery(id+"F0.wireOp",EDGE,"E1")])]}),"instanceName":"1"}),"instanceName":"1"}),"instanceName":"1"}),"instanceName":"1"});
            var Q290;
            Q290=makeQuery(id+"F10.opPattern","COPY",BODY,{"derivedFrom":makeQuery(id+"F9.opPattern","COPY",BODY,{"derivedFrom":makeQuery(id+"F4.opPattern","COPY",BODY,{"derivedFrom":makeQuery(id+"F1.opRevolve","SWEPT_BODY",BODY,{"disambiguationData":[OSD([sQuery(id+"F0.wireOp",EDGE,"E1")])]}),"instanceName":"1"}),"instanceName":"1"}),"instanceName":"1"});
            var Q291;
            Q291=makeQuery(id+"F10.opPattern","COPY",BODY,{"derivedFrom":makeQuery(id+"F9.opPattern","COPY",BODY,{"derivedFrom":makeQuery(id+"F4.opPattern","COPY",BODY,{"derivedFrom":makeQuery(id+"F2.opPattern","COPY",BODY,{"derivedFrom":makeQuery(id+"F1.opRevolve","SWEPT_BODY",BODY,{"disambiguationData":[OSD([sQuery(id+"F0.wireOp",EDGE,"E1")])]}),"instanceName":"1"}),"instanceName":"1"}),"instanceName":"1"}),"instanceName":"1"});
            var Q292;
            Q292=makeQuery(id+"F10.opPattern","COPY",BODY,{"derivedFrom":makeQuery(id+"F9.opPattern","COPY",BODY,{"derivedFrom":makeQuery(id+"F4.opPattern","COPY",BODY,{"derivedFrom":makeQuery(id+"F3.opPattern","COPY",BODY,{"derivedFrom":makeQuery(id+"F2.opPattern","COPY",BODY,{"derivedFrom":makeQuery(id+"F1.opRevolve","SWEPT_BODY",BODY,{"disambiguationData":[OSD([sQuery(id+"F0.wireOp",EDGE,"E1")])]}),"instanceName":"1"}),"instanceName":"1"}),"instanceName":"1"}),"instanceName":"1"}),"instanceName":"1"});
            var Q293;
            Q293=makeQuery(id+"F10.opPattern","COPY",BODY,{"derivedFrom":makeQuery(id+"F9.opPattern","COPY",BODY,{"derivedFrom":makeQuery(id+"F5.opPattern","COPY",BODY,{"derivedFrom":makeQuery(id+"F1.opRevolve","SWEPT_BODY",BODY,{"disambiguationData":[OSD([sQuery(id+"F0.wireOp",EDGE,"E1")])]}),"instanceName":"1"}),"instanceName":"1"}),"instanceName":"1"});
            var Q294;
            Q294=makeQuery(id+"F10.opPattern","COPY",BODY,{"derivedFrom":makeQuery(id+"F9.opPattern","COPY",BODY,{"derivedFrom":makeQuery(id+"F5.opPattern","COPY",BODY,{"derivedFrom":makeQuery(id+"F2.opPattern","COPY",BODY,{"derivedFrom":makeQuery(id+"F1.opRevolve","SWEPT_BODY",BODY,{"disambiguationData":[OSD([sQuery(id+"F0.wireOp",EDGE,"E1")])]}),"instanceName":"1"}),"instanceName":"1"}),"instanceName":"1"}),"instanceName":"1"});
            var Q295;
            Q295=makeQuery(id+"F10.opPattern","COPY",BODY,{"derivedFrom":makeQuery(id+"F9.opPattern","COPY",BODY,{"derivedFrom":makeQuery(id+"F5.opPattern","COPY",BODY,{"derivedFrom":makeQuery(id+"F3.opPattern","COPY",BODY,{"derivedFrom":makeQuery(id+"F2.opPattern","COPY",BODY,{"derivedFrom":makeQuery(id+"F1.opRevolve","SWEPT_BODY",BODY,{"disambiguationData":[OSD([sQuery(id+"F0.wireOp",EDGE,"E1")])]}),"instanceName":"1"}),"instanceName":"1"}),"instanceName":"1"}),"instanceName":"1"}),"instanceName":"1"});
            var Q296;
            Q296=makeQuery(id+"F10.opPattern","COPY",BODY,{"derivedFrom":makeQuery(id+"F9.opPattern","COPY",BODY,{"derivedFrom":makeQuery(id+"F5.opPattern","COPY",BODY,{"derivedFrom":makeQuery(id+"F4.opPattern","COPY",BODY,{"derivedFrom":makeQuery(id+"F1.opRevolve","SWEPT_BODY",BODY,{"disambiguationData":[OSD([sQuery(id+"F0.wireOp",EDGE,"E1")])]}),"instanceName":"1"}),"instanceName":"1"}),"instanceName":"1"}),"instanceName":"1"});
            var Q297;
            Q297=makeQuery(id+"F10.opPattern","COPY",BODY,{"derivedFrom":makeQuery(id+"F9.opPattern","COPY",BODY,{"derivedFrom":makeQuery(id+"F5.opPattern","COPY",BODY,{"derivedFrom":makeQuery(id+"F4.opPattern","COPY",BODY,{"derivedFrom":makeQuery(id+"F2.opPattern","COPY",BODY,{"derivedFrom":makeQuery(id+"F1.opRevolve","SWEPT_BODY",BODY,{"disambiguationData":[OSD([sQuery(id+"F0.wireOp",EDGE,"E1")])]}),"instanceName":"1"}),"instanceName":"1"}),"instanceName":"1"}),"instanceName":"1"}),"instanceName":"1"});
            var Q298;
            Q298=makeQuery(id+"F10.opPattern","COPY",BODY,{"derivedFrom":makeQuery(id+"F9.opPattern","COPY",BODY,{"derivedFrom":makeQuery(id+"F5.opPattern","COPY",BODY,{"derivedFrom":makeQuery(id+"F4.opPattern","COPY",BODY,{"derivedFrom":makeQuery(id+"F3.opPattern","COPY",BODY,{"derivedFrom":makeQuery(id+"F2.opPattern","COPY",BODY,{"derivedFrom":makeQuery(id+"F1.opRevolve","SWEPT_BODY",BODY,{"disambiguationData":[OSD([sQuery(id+"F0.wireOp",EDGE,"E1")])]}),"instanceName":"1"}),"instanceName":"1"}),"instanceName":"1"}),"instanceName":"1"}),"instanceName":"1"}),"instanceName":"1"});
            var Q299;
            Q299=makeQuery(id+"F10.opPattern","COPY",BODY,{"derivedFrom":makeQuery(id+"F9.opPattern","COPY",BODY,{"derivedFrom":makeQuery(id+"F6.opPattern","COPY",BODY,{"derivedFrom":makeQuery(id+"F1.opRevolve","SWEPT_BODY",BODY,{"disambiguationData":[OSD([sQuery(id+"F0.wireOp",EDGE,"E1")])]}),"instanceName":"1"}),"instanceName":"1"}),"instanceName":"1"});
            var Q300;
            Q300=makeQuery(id+"F10.opPattern","COPY",BODY,{"derivedFrom":makeQuery(id+"F9.opPattern","COPY",BODY,{"derivedFrom":makeQuery(id+"F6.opPattern","COPY",BODY,{"derivedFrom":makeQuery(id+"F2.opPattern","COPY",BODY,{"derivedFrom":makeQuery(id+"F1.opRevolve","SWEPT_BODY",BODY,{"disambiguationData":[OSD([sQuery(id+"F0.wireOp",EDGE,"E1")])]}),"instanceName":"1"}),"instanceName":"1"}),"instanceName":"1"}),"instanceName":"1"});
            var Q301;
            Q301=makeQuery(id+"F10.opPattern","COPY",BODY,{"derivedFrom":makeQuery(id+"F9.opPattern","COPY",BODY,{"derivedFrom":makeQuery(id+"F6.opPattern","COPY",BODY,{"derivedFrom":makeQuery(id+"F3.opPattern","COPY",BODY,{"derivedFrom":makeQuery(id+"F2.opPattern","COPY",BODY,{"derivedFrom":makeQuery(id+"F1.opRevolve","SWEPT_BODY",BODY,{"disambiguationData":[OSD([sQuery(id+"F0.wireOp",EDGE,"E1")])]}),"instanceName":"1"}),"instanceName":"1"}),"instanceName":"1"}),"instanceName":"1"}),"instanceName":"1"});
            var Q302;
            Q302=makeQuery(id+"F10.opPattern","COPY",BODY,{"derivedFrom":makeQuery(id+"F9.opPattern","COPY",BODY,{"derivedFrom":makeQuery(id+"F6.opPattern","COPY",BODY,{"derivedFrom":makeQuery(id+"F4.opPattern","COPY",BODY,{"derivedFrom":makeQuery(id+"F1.opRevolve","SWEPT_BODY",BODY,{"disambiguationData":[OSD([sQuery(id+"F0.wireOp",EDGE,"E1")])]}),"instanceName":"1"}),"instanceName":"1"}),"instanceName":"1"}),"instanceName":"1"});
            var Q303;
            Q303=makeQuery(id+"F10.opPattern","COPY",BODY,{"derivedFrom":makeQuery(id+"F9.opPattern","COPY",BODY,{"derivedFrom":makeQuery(id+"F6.opPattern","COPY",BODY,{"derivedFrom":makeQuery(id+"F4.opPattern","COPY",BODY,{"derivedFrom":makeQuery(id+"F2.opPattern","COPY",BODY,{"derivedFrom":makeQuery(id+"F1.opRevolve","SWEPT_BODY",BODY,{"disambiguationData":[OSD([sQuery(id+"F0.wireOp",EDGE,"E1")])]}),"instanceName":"1"}),"instanceName":"1"}),"instanceName":"1"}),"instanceName":"1"}),"instanceName":"1"});
            var Q304;
            Q304=makeQuery(id+"F10.opPattern","COPY",BODY,{"derivedFrom":makeQuery(id+"F9.opPattern","COPY",BODY,{"derivedFrom":makeQuery(id+"F6.opPattern","COPY",BODY,{"derivedFrom":makeQuery(id+"F4.opPattern","COPY",BODY,{"derivedFrom":makeQuery(id+"F3.opPattern","COPY",BODY,{"derivedFrom":makeQuery(id+"F2.opPattern","COPY",BODY,{"derivedFrom":makeQuery(id+"F1.opRevolve","SWEPT_BODY",BODY,{"disambiguationData":[OSD([sQuery(id+"F0.wireOp",EDGE,"E1")])]}),"instanceName":"1"}),"instanceName":"1"}),"instanceName":"1"}),"instanceName":"1"}),"instanceName":"1"}),"instanceName":"1"});
            var Q305;
            Q305=makeQuery(id+"F10.opPattern","COPY",BODY,{"derivedFrom":makeQuery(id+"F9.opPattern","COPY",BODY,{"derivedFrom":makeQuery(id+"F6.opPattern","COPY",BODY,{"derivedFrom":makeQuery(id+"F5.opPattern","COPY",BODY,{"derivedFrom":makeQuery(id+"F1.opRevolve","SWEPT_BODY",BODY,{"disambiguationData":[OSD([sQuery(id+"F0.wireOp",EDGE,"E1")])]}),"instanceName":"1"}),"instanceName":"1"}),"instanceName":"1"}),"instanceName":"1"});
            var Q306;
            Q306=makeQuery(id+"F10.opPattern","COPY",BODY,{"derivedFrom":makeQuery(id+"F9.opPattern","COPY",BODY,{"derivedFrom":makeQuery(id+"F6.opPattern","COPY",BODY,{"derivedFrom":makeQuery(id+"F5.opPattern","COPY",BODY,{"derivedFrom":makeQuery(id+"F2.opPattern","COPY",BODY,{"derivedFrom":makeQuery(id+"F1.opRevolve","SWEPT_BODY",BODY,{"disambiguationData":[OSD([sQuery(id+"F0.wireOp",EDGE,"E1")])]}),"instanceName":"1"}),"instanceName":"1"}),"instanceName":"1"}),"instanceName":"1"}),"instanceName":"1"});
            var Q307;
            Q307=makeQuery(id+"F10.opPattern","COPY",BODY,{"derivedFrom":makeQuery(id+"F9.opPattern","COPY",BODY,{"derivedFrom":makeQuery(id+"F6.opPattern","COPY",BODY,{"derivedFrom":makeQuery(id+"F5.opPattern","COPY",BODY,{"derivedFrom":makeQuery(id+"F3.opPattern","COPY",BODY,{"derivedFrom":makeQuery(id+"F2.opPattern","COPY",BODY,{"derivedFrom":makeQuery(id+"F1.opRevolve","SWEPT_BODY",BODY,{"disambiguationData":[OSD([sQuery(id+"F0.wireOp",EDGE,"E1")])]}),"instanceName":"1"}),"instanceName":"1"}),"instanceName":"1"}),"instanceName":"1"}),"instanceName":"1"}),"instanceName":"1"});
            var Q308;
            Q308=makeQuery(id+"F10.opPattern","COPY",BODY,{"derivedFrom":makeQuery(id+"F9.opPattern","COPY",BODY,{"derivedFrom":makeQuery(id+"F6.opPattern","COPY",BODY,{"derivedFrom":makeQuery(id+"F5.opPattern","COPY",BODY,{"derivedFrom":makeQuery(id+"F4.opPattern","COPY",BODY,{"derivedFrom":makeQuery(id+"F1.opRevolve","SWEPT_BODY",BODY,{"disambiguationData":[OSD([sQuery(id+"F0.wireOp",EDGE,"E1")])]}),"instanceName":"1"}),"instanceName":"1"}),"instanceName":"1"}),"instanceName":"1"}),"instanceName":"1"});
            var Q309;
            Q309=makeQuery(id+"F10.opPattern","COPY",BODY,{"derivedFrom":makeQuery(id+"F9.opPattern","COPY",BODY,{"derivedFrom":makeQuery(id+"F6.opPattern","COPY",BODY,{"derivedFrom":makeQuery(id+"F5.opPattern","COPY",BODY,{"derivedFrom":makeQuery(id+"F4.opPattern","COPY",BODY,{"derivedFrom":makeQuery(id+"F2.opPattern","COPY",BODY,{"derivedFrom":makeQuery(id+"F1.opRevolve","SWEPT_BODY",BODY,{"disambiguationData":[OSD([sQuery(id+"F0.wireOp",EDGE,"E1")])]}),"instanceName":"1"}),"instanceName":"1"}),"instanceName":"1"}),"instanceName":"1"}),"instanceName":"1"}),"instanceName":"1"});
            var Q310;
            Q310=makeQuery(id+"F10.opPattern","COPY",BODY,{"derivedFrom":makeQuery(id+"F9.opPattern","COPY",BODY,{"derivedFrom":makeQuery(id+"F6.opPattern","COPY",BODY,{"derivedFrom":makeQuery(id+"F5.opPattern","COPY",BODY,{"derivedFrom":makeQuery(id+"F4.opPattern","COPY",BODY,{"derivedFrom":makeQuery(id+"F3.opPattern","COPY",BODY,{"derivedFrom":makeQuery(id+"F2.opPattern","COPY",BODY,{"derivedFrom":makeQuery(id+"F1.opRevolve","SWEPT_BODY",BODY,{"disambiguationData":[OSD([sQuery(id+"F0.wireOp",EDGE,"E1")])]}),"instanceName":"1"}),"instanceName":"1"}),"instanceName":"1"}),"instanceName":"1"}),"instanceName":"1"}),"instanceName":"1"}),"instanceName":"1"});
            var Q311;
            Q311=makeQuery(id+"F10.opPattern","COPY",BODY,{"derivedFrom":makeQuery(id+"F9.opPattern","COPY",BODY,{"derivedFrom":makeQuery(id+"F7.opPattern","COPY",BODY,{"derivedFrom":makeQuery(id+"F1.opRevolve","SWEPT_BODY",BODY,{"disambiguationData":[OSD([sQuery(id+"F0.wireOp",EDGE,"E1")])]}),"instanceName":"1"}),"instanceName":"1"}),"instanceName":"1"});
            var Q312;
            Q312=makeQuery(id+"F10.opPattern","COPY",BODY,{"derivedFrom":makeQuery(id+"F9.opPattern","COPY",BODY,{"derivedFrom":makeQuery(id+"F7.opPattern","COPY",BODY,{"derivedFrom":makeQuery(id+"F2.opPattern","COPY",BODY,{"derivedFrom":makeQuery(id+"F1.opRevolve","SWEPT_BODY",BODY,{"disambiguationData":[OSD([sQuery(id+"F0.wireOp",EDGE,"E1")])]}),"instanceName":"1"}),"instanceName":"1"}),"instanceName":"1"}),"instanceName":"1"});
            var Q313;
            Q313=makeQuery(id+"F10.opPattern","COPY",BODY,{"derivedFrom":makeQuery(id+"F9.opPattern","COPY",BODY,{"derivedFrom":makeQuery(id+"F7.opPattern","COPY",BODY,{"derivedFrom":makeQuery(id+"F3.opPattern","COPY",BODY,{"derivedFrom":makeQuery(id+"F2.opPattern","COPY",BODY,{"derivedFrom":makeQuery(id+"F1.opRevolve","SWEPT_BODY",BODY,{"disambiguationData":[OSD([sQuery(id+"F0.wireOp",EDGE,"E1")])]}),"instanceName":"1"}),"instanceName":"1"}),"instanceName":"1"}),"instanceName":"1"}),"instanceName":"1"});
            var Q314;
            Q314=makeQuery(id+"F10.opPattern","COPY",BODY,{"derivedFrom":makeQuery(id+"F9.opPattern","COPY",BODY,{"derivedFrom":makeQuery(id+"F7.opPattern","COPY",BODY,{"derivedFrom":makeQuery(id+"F4.opPattern","COPY",BODY,{"derivedFrom":makeQuery(id+"F1.opRevolve","SWEPT_BODY",BODY,{"disambiguationData":[OSD([sQuery(id+"F0.wireOp",EDGE,"E1")])]}),"instanceName":"1"}),"instanceName":"1"}),"instanceName":"1"}),"instanceName":"1"});
            var Q315;
            Q315=makeQuery(id+"F10.opPattern","COPY",BODY,{"derivedFrom":makeQuery(id+"F9.opPattern","COPY",BODY,{"derivedFrom":makeQuery(id+"F7.opPattern","COPY",BODY,{"derivedFrom":makeQuery(id+"F4.opPattern","COPY",BODY,{"derivedFrom":makeQuery(id+"F2.opPattern","COPY",BODY,{"derivedFrom":makeQuery(id+"F1.opRevolve","SWEPT_BODY",BODY,{"disambiguationData":[OSD([sQuery(id+"F0.wireOp",EDGE,"E1")])]}),"instanceName":"1"}),"instanceName":"1"}),"instanceName":"1"}),"instanceName":"1"}),"instanceName":"1"});
            var Q316;
            Q316=makeQuery(id+"F10.opPattern","COPY",BODY,{"derivedFrom":makeQuery(id+"F9.opPattern","COPY",BODY,{"derivedFrom":makeQuery(id+"F7.opPattern","COPY",BODY,{"derivedFrom":makeQuery(id+"F4.opPattern","COPY",BODY,{"derivedFrom":makeQuery(id+"F3.opPattern","COPY",BODY,{"derivedFrom":makeQuery(id+"F2.opPattern","COPY",BODY,{"derivedFrom":makeQuery(id+"F1.opRevolve","SWEPT_BODY",BODY,{"disambiguationData":[OSD([sQuery(id+"F0.wireOp",EDGE,"E1")])]}),"instanceName":"1"}),"instanceName":"1"}),"instanceName":"1"}),"instanceName":"1"}),"instanceName":"1"}),"instanceName":"1"});
            var Q317;
            Q317=makeQuery(id+"F10.opPattern","COPY",BODY,{"derivedFrom":makeQuery(id+"F9.opPattern","COPY",BODY,{"derivedFrom":makeQuery(id+"F7.opPattern","COPY",BODY,{"derivedFrom":makeQuery(id+"F5.opPattern","COPY",BODY,{"derivedFrom":makeQuery(id+"F1.opRevolve","SWEPT_BODY",BODY,{"disambiguationData":[OSD([sQuery(id+"F0.wireOp",EDGE,"E1")])]}),"instanceName":"1"}),"instanceName":"1"}),"instanceName":"1"}),"instanceName":"1"});
            var Q318;
            Q318=makeQuery(id+"F10.opPattern","COPY",BODY,{"derivedFrom":makeQuery(id+"F9.opPattern","COPY",BODY,{"derivedFrom":makeQuery(id+"F7.opPattern","COPY",BODY,{"derivedFrom":makeQuery(id+"F5.opPattern","COPY",BODY,{"derivedFrom":makeQuery(id+"F2.opPattern","COPY",BODY,{"derivedFrom":makeQuery(id+"F1.opRevolve","SWEPT_BODY",BODY,{"disambiguationData":[OSD([sQuery(id+"F0.wireOp",EDGE,"E1")])]}),"instanceName":"1"}),"instanceName":"1"}),"instanceName":"1"}),"instanceName":"1"}),"instanceName":"1"});
            var Q319;
            Q319=makeQuery(id+"F10.opPattern","COPY",BODY,{"derivedFrom":makeQuery(id+"F9.opPattern","COPY",BODY,{"derivedFrom":makeQuery(id+"F7.opPattern","COPY",BODY,{"derivedFrom":makeQuery(id+"F5.opPattern","COPY",BODY,{"derivedFrom":makeQuery(id+"F3.opPattern","COPY",BODY,{"derivedFrom":makeQuery(id+"F2.opPattern","COPY",BODY,{"derivedFrom":makeQuery(id+"F1.opRevolve","SWEPT_BODY",BODY,{"disambiguationData":[OSD([sQuery(id+"F0.wireOp",EDGE,"E1")])]}),"instanceName":"1"}),"instanceName":"1"}),"instanceName":"1"}),"instanceName":"1"}),"instanceName":"1"}),"instanceName":"1"});
            var Q320;
            Q320=makeQuery(id+"F10.opPattern","COPY",BODY,{"derivedFrom":makeQuery(id+"F9.opPattern","COPY",BODY,{"derivedFrom":makeQuery(id+"F7.opPattern","COPY",BODY,{"derivedFrom":makeQuery(id+"F5.opPattern","COPY",BODY,{"derivedFrom":makeQuery(id+"F4.opPattern","COPY",BODY,{"derivedFrom":makeQuery(id+"F1.opRevolve","SWEPT_BODY",BODY,{"disambiguationData":[OSD([sQuery(id+"F0.wireOp",EDGE,"E1")])]}),"instanceName":"1"}),"instanceName":"1"}),"instanceName":"1"}),"instanceName":"1"}),"instanceName":"1"});
            var Q321;
            Q321=makeQuery(id+"F10.opPattern","COPY",BODY,{"derivedFrom":makeQuery(id+"F9.opPattern","COPY",BODY,{"derivedFrom":makeQuery(id+"F7.opPattern","COPY",BODY,{"derivedFrom":makeQuery(id+"F5.opPattern","COPY",BODY,{"derivedFrom":makeQuery(id+"F4.opPattern","COPY",BODY,{"derivedFrom":makeQuery(id+"F2.opPattern","COPY",BODY,{"derivedFrom":makeQuery(id+"F1.opRevolve","SWEPT_BODY",BODY,{"disambiguationData":[OSD([sQuery(id+"F0.wireOp",EDGE,"E1")])]}),"instanceName":"1"}),"instanceName":"1"}),"instanceName":"1"}),"instanceName":"1"}),"instanceName":"1"}),"instanceName":"1"});
            var Q322;
            Q322=makeQuery(id+"F10.opPattern","COPY",BODY,{"derivedFrom":makeQuery(id+"F9.opPattern","COPY",BODY,{"derivedFrom":makeQuery(id+"F7.opPattern","COPY",BODY,{"derivedFrom":makeQuery(id+"F5.opPattern","COPY",BODY,{"derivedFrom":makeQuery(id+"F4.opPattern","COPY",BODY,{"derivedFrom":makeQuery(id+"F3.opPattern","COPY",BODY,{"derivedFrom":makeQuery(id+"F2.opPattern","COPY",BODY,{"derivedFrom":makeQuery(id+"F1.opRevolve","SWEPT_BODY",BODY,{"disambiguationData":[OSD([sQuery(id+"F0.wireOp",EDGE,"E1")])]}),"instanceName":"1"}),"instanceName":"1"}),"instanceName":"1"}),"instanceName":"1"}),"instanceName":"1"}),"instanceName":"1"}),"instanceName":"1"});
            var Q323;
            Q323=makeQuery(id+"F10.opPattern","COPY",BODY,{"derivedFrom":makeQuery(id+"F9.opPattern","COPY",BODY,{"derivedFrom":makeQuery(id+"F7.opPattern","COPY",BODY,{"derivedFrom":makeQuery(id+"F6.opPattern","COPY",BODY,{"derivedFrom":makeQuery(id+"F1.opRevolve","SWEPT_BODY",BODY,{"disambiguationData":[OSD([sQuery(id+"F0.wireOp",EDGE,"E1")])]}),"instanceName":"1"}),"instanceName":"1"}),"instanceName":"1"}),"instanceName":"1"});
            var Q324;
            Q324=makeQuery(id+"F10.opPattern","COPY",BODY,{"derivedFrom":makeQuery(id+"F9.opPattern","COPY",BODY,{"derivedFrom":makeQuery(id+"F7.opPattern","COPY",BODY,{"derivedFrom":makeQuery(id+"F6.opPattern","COPY",BODY,{"derivedFrom":makeQuery(id+"F2.opPattern","COPY",BODY,{"derivedFrom":makeQuery(id+"F1.opRevolve","SWEPT_BODY",BODY,{"disambiguationData":[OSD([sQuery(id+"F0.wireOp",EDGE,"E1")])]}),"instanceName":"1"}),"instanceName":"1"}),"instanceName":"1"}),"instanceName":"1"}),"instanceName":"1"});
            var Q325;
            Q325=makeQuery(id+"F10.opPattern","COPY",BODY,{"derivedFrom":makeQuery(id+"F9.opPattern","COPY",BODY,{"derivedFrom":makeQuery(id+"F7.opPattern","COPY",BODY,{"derivedFrom":makeQuery(id+"F6.opPattern","COPY",BODY,{"derivedFrom":makeQuery(id+"F3.opPattern","COPY",BODY,{"derivedFrom":makeQuery(id+"F2.opPattern","COPY",BODY,{"derivedFrom":makeQuery(id+"F1.opRevolve","SWEPT_BODY",BODY,{"disambiguationData":[OSD([sQuery(id+"F0.wireOp",EDGE,"E1")])]}),"instanceName":"1"}),"instanceName":"1"}),"instanceName":"1"}),"instanceName":"1"}),"instanceName":"1"}),"instanceName":"1"});
            var Q326;
            Q326=makeQuery(id+"F10.opPattern","COPY",BODY,{"derivedFrom":makeQuery(id+"F9.opPattern","COPY",BODY,{"derivedFrom":makeQuery(id+"F7.opPattern","COPY",BODY,{"derivedFrom":makeQuery(id+"F6.opPattern","COPY",BODY,{"derivedFrom":makeQuery(id+"F4.opPattern","COPY",BODY,{"derivedFrom":makeQuery(id+"F1.opRevolve","SWEPT_BODY",BODY,{"disambiguationData":[OSD([sQuery(id+"F0.wireOp",EDGE,"E1")])]}),"instanceName":"1"}),"instanceName":"1"}),"instanceName":"1"}),"instanceName":"1"}),"instanceName":"1"});
            var Q327;
            Q327=makeQuery(id+"F10.opPattern","COPY",BODY,{"derivedFrom":makeQuery(id+"F9.opPattern","COPY",BODY,{"derivedFrom":makeQuery(id+"F7.opPattern","COPY",BODY,{"derivedFrom":makeQuery(id+"F6.opPattern","COPY",BODY,{"derivedFrom":makeQuery(id+"F4.opPattern","COPY",BODY,{"derivedFrom":makeQuery(id+"F2.opPattern","COPY",BODY,{"derivedFrom":makeQuery(id+"F1.opRevolve","SWEPT_BODY",BODY,{"disambiguationData":[OSD([sQuery(id+"F0.wireOp",EDGE,"E1")])]}),"instanceName":"1"}),"instanceName":"1"}),"instanceName":"1"}),"instanceName":"1"}),"instanceName":"1"}),"instanceName":"1"});
            var Q328;
            Q328=makeQuery(id+"F10.opPattern","COPY",BODY,{"derivedFrom":makeQuery(id+"F9.opPattern","COPY",BODY,{"derivedFrom":makeQuery(id+"F7.opPattern","COPY",BODY,{"derivedFrom":makeQuery(id+"F6.opPattern","COPY",BODY,{"derivedFrom":makeQuery(id+"F4.opPattern","COPY",BODY,{"derivedFrom":makeQuery(id+"F3.opPattern","COPY",BODY,{"derivedFrom":makeQuery(id+"F2.opPattern","COPY",BODY,{"derivedFrom":makeQuery(id+"F1.opRevolve","SWEPT_BODY",BODY,{"disambiguationData":[OSD([sQuery(id+"F0.wireOp",EDGE,"E1")])]}),"instanceName":"1"}),"instanceName":"1"}),"instanceName":"1"}),"instanceName":"1"}),"instanceName":"1"}),"instanceName":"1"}),"instanceName":"1"});
            var Q329;
            Q329=makeQuery(id+"F10.opPattern","COPY",BODY,{"derivedFrom":makeQuery(id+"F9.opPattern","COPY",BODY,{"derivedFrom":makeQuery(id+"F7.opPattern","COPY",BODY,{"derivedFrom":makeQuery(id+"F6.opPattern","COPY",BODY,{"derivedFrom":makeQuery(id+"F5.opPattern","COPY",BODY,{"derivedFrom":makeQuery(id+"F1.opRevolve","SWEPT_BODY",BODY,{"disambiguationData":[OSD([sQuery(id+"F0.wireOp",EDGE,"E1")])]}),"instanceName":"1"}),"instanceName":"1"}),"instanceName":"1"}),"instanceName":"1"}),"instanceName":"1"});
            var Q330;
            Q330=makeQuery(id+"F10.opPattern","COPY",BODY,{"derivedFrom":makeQuery(id+"F9.opPattern","COPY",BODY,{"derivedFrom":makeQuery(id+"F7.opPattern","COPY",BODY,{"derivedFrom":makeQuery(id+"F6.opPattern","COPY",BODY,{"derivedFrom":makeQuery(id+"F5.opPattern","COPY",BODY,{"derivedFrom":makeQuery(id+"F2.opPattern","COPY",BODY,{"derivedFrom":makeQuery(id+"F1.opRevolve","SWEPT_BODY",BODY,{"disambiguationData":[OSD([sQuery(id+"F0.wireOp",EDGE,"E1")])]}),"instanceName":"1"}),"instanceName":"1"}),"instanceName":"1"}),"instanceName":"1"}),"instanceName":"1"}),"instanceName":"1"});
            var Q331;
            Q331=makeQuery(id+"F10.opPattern","COPY",BODY,{"derivedFrom":makeQuery(id+"F9.opPattern","COPY",BODY,{"derivedFrom":makeQuery(id+"F7.opPattern","COPY",BODY,{"derivedFrom":makeQuery(id+"F6.opPattern","COPY",BODY,{"derivedFrom":makeQuery(id+"F5.opPattern","COPY",BODY,{"derivedFrom":makeQuery(id+"F3.opPattern","COPY",BODY,{"derivedFrom":makeQuery(id+"F2.opPattern","COPY",BODY,{"derivedFrom":makeQuery(id+"F1.opRevolve","SWEPT_BODY",BODY,{"disambiguationData":[OSD([sQuery(id+"F0.wireOp",EDGE,"E1")])]}),"instanceName":"1"}),"instanceName":"1"}),"instanceName":"1"}),"instanceName":"1"}),"instanceName":"1"}),"instanceName":"1"}),"instanceName":"1"});
            var Q332;
            Q332=makeQuery(id+"F10.opPattern","COPY",BODY,{"derivedFrom":makeQuery(id+"F9.opPattern","COPY",BODY,{"derivedFrom":makeQuery(id+"F7.opPattern","COPY",BODY,{"derivedFrom":makeQuery(id+"F6.opPattern","COPY",BODY,{"derivedFrom":makeQuery(id+"F5.opPattern","COPY",BODY,{"derivedFrom":makeQuery(id+"F4.opPattern","COPY",BODY,{"derivedFrom":makeQuery(id+"F1.opRevolve","SWEPT_BODY",BODY,{"disambiguationData":[OSD([sQuery(id+"F0.wireOp",EDGE,"E1")])]}),"instanceName":"1"}),"instanceName":"1"}),"instanceName":"1"}),"instanceName":"1"}),"instanceName":"1"}),"instanceName":"1"});
            var Q333;
            Q333=makeQuery(id+"F10.opPattern","COPY",BODY,{"derivedFrom":makeQuery(id+"F9.opPattern","COPY",BODY,{"derivedFrom":makeQuery(id+"F7.opPattern","COPY",BODY,{"derivedFrom":makeQuery(id+"F6.opPattern","COPY",BODY,{"derivedFrom":makeQuery(id+"F5.opPattern","COPY",BODY,{"derivedFrom":makeQuery(id+"F4.opPattern","COPY",BODY,{"derivedFrom":makeQuery(id+"F2.opPattern","COPY",BODY,{"derivedFrom":makeQuery(id+"F1.opRevolve","SWEPT_BODY",BODY,{"disambiguationData":[OSD([sQuery(id+"F0.wireOp",EDGE,"E1")])]}),"instanceName":"1"}),"instanceName":"1"}),"instanceName":"1"}),"instanceName":"1"}),"instanceName":"1"}),"instanceName":"1"}),"instanceName":"1"});
            var Q334;
            Q334=makeQuery(id+"F10.opPattern","COPY",BODY,{"derivedFrom":makeQuery(id+"F9.opPattern","COPY",BODY,{"derivedFrom":makeQuery(id+"F7.opPattern","COPY",BODY,{"derivedFrom":makeQuery(id+"F6.opPattern","COPY",BODY,{"derivedFrom":makeQuery(id+"F5.opPattern","COPY",BODY,{"derivedFrom":makeQuery(id+"F4.opPattern","COPY",BODY,{"derivedFrom":makeQuery(id+"F3.opPattern","COPY",BODY,{"derivedFrom":makeQuery(id+"F2.opPattern","COPY",BODY,{"derivedFrom":makeQuery(id+"F1.opRevolve","SWEPT_BODY",BODY,{"disambiguationData":[OSD([sQuery(id+"F0.wireOp",EDGE,"E1")])]}),"instanceName":"1"}),"instanceName":"1"}),"instanceName":"1"}),"instanceName":"1"}),"instanceName":"1"}),"instanceName":"1"}),"instanceName":"1"}),"instanceName":"1"});
            var Q335;
            Q335=makeQuery(id+"F10.opPattern","COPY",BODY,{"derivedFrom":makeQuery(id+"F9.opPattern","COPY",BODY,{"derivedFrom":makeQuery(id+"F8.opPattern","COPY",BODY,{"derivedFrom":makeQuery(id+"F1.opRevolve","SWEPT_BODY",BODY,{"disambiguationData":[OSD([sQuery(id+"F0.wireOp",EDGE,"E1")])]}),"instanceName":"1"}),"instanceName":"1"}),"instanceName":"1"});
            var Q336;
            Q336=makeQuery(id+"F10.opPattern","COPY",BODY,{"derivedFrom":makeQuery(id+"F9.opPattern","COPY",BODY,{"derivedFrom":makeQuery(id+"F8.opPattern","COPY",BODY,{"derivedFrom":makeQuery(id+"F2.opPattern","COPY",BODY,{"derivedFrom":makeQuery(id+"F1.opRevolve","SWEPT_BODY",BODY,{"disambiguationData":[OSD([sQuery(id+"F0.wireOp",EDGE,"E1")])]}),"instanceName":"1"}),"instanceName":"1"}),"instanceName":"1"}),"instanceName":"1"});
            var Q337;
            Q337=makeQuery(id+"F10.opPattern","COPY",BODY,{"derivedFrom":makeQuery(id+"F9.opPattern","COPY",BODY,{"derivedFrom":makeQuery(id+"F8.opPattern","COPY",BODY,{"derivedFrom":makeQuery(id+"F3.opPattern","COPY",BODY,{"derivedFrom":makeQuery(id+"F2.opPattern","COPY",BODY,{"derivedFrom":makeQuery(id+"F1.opRevolve","SWEPT_BODY",BODY,{"disambiguationData":[OSD([sQuery(id+"F0.wireOp",EDGE,"E1")])]}),"instanceName":"1"}),"instanceName":"1"}),"instanceName":"1"}),"instanceName":"1"}),"instanceName":"1"});
            var Q338;
            Q338=makeQuery(id+"F10.opPattern","COPY",BODY,{"derivedFrom":makeQuery(id+"F9.opPattern","COPY",BODY,{"derivedFrom":makeQuery(id+"F8.opPattern","COPY",BODY,{"derivedFrom":makeQuery(id+"F4.opPattern","COPY",BODY,{"derivedFrom":makeQuery(id+"F1.opRevolve","SWEPT_BODY",BODY,{"disambiguationData":[OSD([sQuery(id+"F0.wireOp",EDGE,"E1")])]}),"instanceName":"1"}),"instanceName":"1"}),"instanceName":"1"}),"instanceName":"1"});
            var Q339;
            Q339=makeQuery(id+"F10.opPattern","COPY",BODY,{"derivedFrom":makeQuery(id+"F9.opPattern","COPY",BODY,{"derivedFrom":makeQuery(id+"F8.opPattern","COPY",BODY,{"derivedFrom":makeQuery(id+"F4.opPattern","COPY",BODY,{"derivedFrom":makeQuery(id+"F2.opPattern","COPY",BODY,{"derivedFrom":makeQuery(id+"F1.opRevolve","SWEPT_BODY",BODY,{"disambiguationData":[OSD([sQuery(id+"F0.wireOp",EDGE,"E1")])]}),"instanceName":"1"}),"instanceName":"1"}),"instanceName":"1"}),"instanceName":"1"}),"instanceName":"1"});
            var Q340;
            Q340=makeQuery(id+"F10.opPattern","COPY",BODY,{"derivedFrom":makeQuery(id+"F9.opPattern","COPY",BODY,{"derivedFrom":makeQuery(id+"F8.opPattern","COPY",BODY,{"derivedFrom":makeQuery(id+"F4.opPattern","COPY",BODY,{"derivedFrom":makeQuery(id+"F3.opPattern","COPY",BODY,{"derivedFrom":makeQuery(id+"F2.opPattern","COPY",BODY,{"derivedFrom":makeQuery(id+"F1.opRevolve","SWEPT_BODY",BODY,{"disambiguationData":[OSD([sQuery(id+"F0.wireOp",EDGE,"E1")])]}),"instanceName":"1"}),"instanceName":"1"}),"instanceName":"1"}),"instanceName":"1"}),"instanceName":"1"}),"instanceName":"1"});
            var Q341;
            Q341=makeQuery(id+"F10.opPattern","COPY",BODY,{"derivedFrom":makeQuery(id+"F9.opPattern","COPY",BODY,{"derivedFrom":makeQuery(id+"F8.opPattern","COPY",BODY,{"derivedFrom":makeQuery(id+"F5.opPattern","COPY",BODY,{"derivedFrom":makeQuery(id+"F1.opRevolve","SWEPT_BODY",BODY,{"disambiguationData":[OSD([sQuery(id+"F0.wireOp",EDGE,"E1")])]}),"instanceName":"1"}),"instanceName":"1"}),"instanceName":"1"}),"instanceName":"1"});
            var Q342;
            Q342=makeQuery(id+"F10.opPattern","COPY",BODY,{"derivedFrom":makeQuery(id+"F9.opPattern","COPY",BODY,{"derivedFrom":makeQuery(id+"F8.opPattern","COPY",BODY,{"derivedFrom":makeQuery(id+"F5.opPattern","COPY",BODY,{"derivedFrom":makeQuery(id+"F2.opPattern","COPY",BODY,{"derivedFrom":makeQuery(id+"F1.opRevolve","SWEPT_BODY",BODY,{"disambiguationData":[OSD([sQuery(id+"F0.wireOp",EDGE,"E1")])]}),"instanceName":"1"}),"instanceName":"1"}),"instanceName":"1"}),"instanceName":"1"}),"instanceName":"1"});
            var Q343;
            Q343=makeQuery(id+"F10.opPattern","COPY",BODY,{"derivedFrom":makeQuery(id+"F9.opPattern","COPY",BODY,{"derivedFrom":makeQuery(id+"F8.opPattern","COPY",BODY,{"derivedFrom":makeQuery(id+"F5.opPattern","COPY",BODY,{"derivedFrom":makeQuery(id+"F3.opPattern","COPY",BODY,{"derivedFrom":makeQuery(id+"F2.opPattern","COPY",BODY,{"derivedFrom":makeQuery(id+"F1.opRevolve","SWEPT_BODY",BODY,{"disambiguationData":[OSD([sQuery(id+"F0.wireOp",EDGE,"E1")])]}),"instanceName":"1"}),"instanceName":"1"}),"instanceName":"1"}),"instanceName":"1"}),"instanceName":"1"}),"instanceName":"1"});
            var Q344;
            Q344=makeQuery(id+"F10.opPattern","COPY",BODY,{"derivedFrom":makeQuery(id+"F9.opPattern","COPY",BODY,{"derivedFrom":makeQuery(id+"F8.opPattern","COPY",BODY,{"derivedFrom":makeQuery(id+"F5.opPattern","COPY",BODY,{"derivedFrom":makeQuery(id+"F4.opPattern","COPY",BODY,{"derivedFrom":makeQuery(id+"F1.opRevolve","SWEPT_BODY",BODY,{"disambiguationData":[OSD([sQuery(id+"F0.wireOp",EDGE,"E1")])]}),"instanceName":"1"}),"instanceName":"1"}),"instanceName":"1"}),"instanceName":"1"}),"instanceName":"1"});
            var Q345;
            Q345=makeQuery(id+"F10.opPattern","COPY",BODY,{"derivedFrom":makeQuery(id+"F9.opPattern","COPY",BODY,{"derivedFrom":makeQuery(id+"F8.opPattern","COPY",BODY,{"derivedFrom":makeQuery(id+"F5.opPattern","COPY",BODY,{"derivedFrom":makeQuery(id+"F4.opPattern","COPY",BODY,{"derivedFrom":makeQuery(id+"F2.opPattern","COPY",BODY,{"derivedFrom":makeQuery(id+"F1.opRevolve","SWEPT_BODY",BODY,{"disambiguationData":[OSD([sQuery(id+"F0.wireOp",EDGE,"E1")])]}),"instanceName":"1"}),"instanceName":"1"}),"instanceName":"1"}),"instanceName":"1"}),"instanceName":"1"}),"instanceName":"1"});
            var Q346;
            Q346=makeQuery(id+"F10.opPattern","COPY",BODY,{"derivedFrom":makeQuery(id+"F9.opPattern","COPY",BODY,{"derivedFrom":makeQuery(id+"F8.opPattern","COPY",BODY,{"derivedFrom":makeQuery(id+"F5.opPattern","COPY",BODY,{"derivedFrom":makeQuery(id+"F4.opPattern","COPY",BODY,{"derivedFrom":makeQuery(id+"F3.opPattern","COPY",BODY,{"derivedFrom":makeQuery(id+"F2.opPattern","COPY",BODY,{"derivedFrom":makeQuery(id+"F1.opRevolve","SWEPT_BODY",BODY,{"disambiguationData":[OSD([sQuery(id+"F0.wireOp",EDGE,"E1")])]}),"instanceName":"1"}),"instanceName":"1"}),"instanceName":"1"}),"instanceName":"1"}),"instanceName":"1"}),"instanceName":"1"}),"instanceName":"1"});
            var Q347;
            Q347=makeQuery(id+"F10.opPattern","COPY",BODY,{"derivedFrom":makeQuery(id+"F9.opPattern","COPY",BODY,{"derivedFrom":makeQuery(id+"F8.opPattern","COPY",BODY,{"derivedFrom":makeQuery(id+"F6.opPattern","COPY",BODY,{"derivedFrom":makeQuery(id+"F1.opRevolve","SWEPT_BODY",BODY,{"disambiguationData":[OSD([sQuery(id+"F0.wireOp",EDGE,"E1")])]}),"instanceName":"1"}),"instanceName":"1"}),"instanceName":"1"}),"instanceName":"1"});
            var Q348;
            Q348=makeQuery(id+"F10.opPattern","COPY",BODY,{"derivedFrom":makeQuery(id+"F9.opPattern","COPY",BODY,{"derivedFrom":makeQuery(id+"F8.opPattern","COPY",BODY,{"derivedFrom":makeQuery(id+"F6.opPattern","COPY",BODY,{"derivedFrom":makeQuery(id+"F2.opPattern","COPY",BODY,{"derivedFrom":makeQuery(id+"F1.opRevolve","SWEPT_BODY",BODY,{"disambiguationData":[OSD([sQuery(id+"F0.wireOp",EDGE,"E1")])]}),"instanceName":"1"}),"instanceName":"1"}),"instanceName":"1"}),"instanceName":"1"}),"instanceName":"1"});
            var Q349;
            Q349=makeQuery(id+"F10.opPattern","COPY",BODY,{"derivedFrom":makeQuery(id+"F9.opPattern","COPY",BODY,{"derivedFrom":makeQuery(id+"F8.opPattern","COPY",BODY,{"derivedFrom":makeQuery(id+"F6.opPattern","COPY",BODY,{"derivedFrom":makeQuery(id+"F3.opPattern","COPY",BODY,{"derivedFrom":makeQuery(id+"F2.opPattern","COPY",BODY,{"derivedFrom":makeQuery(id+"F1.opRevolve","SWEPT_BODY",BODY,{"disambiguationData":[OSD([sQuery(id+"F0.wireOp",EDGE,"E1")])]}),"instanceName":"1"}),"instanceName":"1"}),"instanceName":"1"}),"instanceName":"1"}),"instanceName":"1"}),"instanceName":"1"});
            var Q350;
            Q350=makeQuery(id+"F10.opPattern","COPY",BODY,{"derivedFrom":makeQuery(id+"F9.opPattern","COPY",BODY,{"derivedFrom":makeQuery(id+"F8.opPattern","COPY",BODY,{"derivedFrom":makeQuery(id+"F6.opPattern","COPY",BODY,{"derivedFrom":makeQuery(id+"F4.opPattern","COPY",BODY,{"derivedFrom":makeQuery(id+"F1.opRevolve","SWEPT_BODY",BODY,{"disambiguationData":[OSD([sQuery(id+"F0.wireOp",EDGE,"E1")])]}),"instanceName":"1"}),"instanceName":"1"}),"instanceName":"1"}),"instanceName":"1"}),"instanceName":"1"});
            var Q351;
            Q351=makeQuery(id+"F10.opPattern","COPY",BODY,{"derivedFrom":makeQuery(id+"F9.opPattern","COPY",BODY,{"derivedFrom":makeQuery(id+"F8.opPattern","COPY",BODY,{"derivedFrom":makeQuery(id+"F6.opPattern","COPY",BODY,{"derivedFrom":makeQuery(id+"F4.opPattern","COPY",BODY,{"derivedFrom":makeQuery(id+"F2.opPattern","COPY",BODY,{"derivedFrom":makeQuery(id+"F1.opRevolve","SWEPT_BODY",BODY,{"disambiguationData":[OSD([sQuery(id+"F0.wireOp",EDGE,"E1")])]}),"instanceName":"1"}),"instanceName":"1"}),"instanceName":"1"}),"instanceName":"1"}),"instanceName":"1"}),"instanceName":"1"});
            var Q352;
            Q352=makeQuery(id+"F10.opPattern","COPY",BODY,{"derivedFrom":makeQuery(id+"F9.opPattern","COPY",BODY,{"derivedFrom":makeQuery(id+"F8.opPattern","COPY",BODY,{"derivedFrom":makeQuery(id+"F6.opPattern","COPY",BODY,{"derivedFrom":makeQuery(id+"F4.opPattern","COPY",BODY,{"derivedFrom":makeQuery(id+"F3.opPattern","COPY",BODY,{"derivedFrom":makeQuery(id+"F2.opPattern","COPY",BODY,{"derivedFrom":makeQuery(id+"F1.opRevolve","SWEPT_BODY",BODY,{"disambiguationData":[OSD([sQuery(id+"F0.wireOp",EDGE,"E1")])]}),"instanceName":"1"}),"instanceName":"1"}),"instanceName":"1"}),"instanceName":"1"}),"instanceName":"1"}),"instanceName":"1"}),"instanceName":"1"});
            var Q353;
            Q353=makeQuery(id+"F10.opPattern","COPY",BODY,{"derivedFrom":makeQuery(id+"F9.opPattern","COPY",BODY,{"derivedFrom":makeQuery(id+"F8.opPattern","COPY",BODY,{"derivedFrom":makeQuery(id+"F6.opPattern","COPY",BODY,{"derivedFrom":makeQuery(id+"F5.opPattern","COPY",BODY,{"derivedFrom":makeQuery(id+"F1.opRevolve","SWEPT_BODY",BODY,{"disambiguationData":[OSD([sQuery(id+"F0.wireOp",EDGE,"E1")])]}),"instanceName":"1"}),"instanceName":"1"}),"instanceName":"1"}),"instanceName":"1"}),"instanceName":"1"});
            var Q354;
            Q354=makeQuery(id+"F10.opPattern","COPY",BODY,{"derivedFrom":makeQuery(id+"F9.opPattern","COPY",BODY,{"derivedFrom":makeQuery(id+"F8.opPattern","COPY",BODY,{"derivedFrom":makeQuery(id+"F6.opPattern","COPY",BODY,{"derivedFrom":makeQuery(id+"F5.opPattern","COPY",BODY,{"derivedFrom":makeQuery(id+"F2.opPattern","COPY",BODY,{"derivedFrom":makeQuery(id+"F1.opRevolve","SWEPT_BODY",BODY,{"disambiguationData":[OSD([sQuery(id+"F0.wireOp",EDGE,"E1")])]}),"instanceName":"1"}),"instanceName":"1"}),"instanceName":"1"}),"instanceName":"1"}),"instanceName":"1"}),"instanceName":"1"});
            var Q355;
            Q355=makeQuery(id+"F10.opPattern","COPY",BODY,{"derivedFrom":makeQuery(id+"F9.opPattern","COPY",BODY,{"derivedFrom":makeQuery(id+"F8.opPattern","COPY",BODY,{"derivedFrom":makeQuery(id+"F6.opPattern","COPY",BODY,{"derivedFrom":makeQuery(id+"F5.opPattern","COPY",BODY,{"derivedFrom":makeQuery(id+"F3.opPattern","COPY",BODY,{"derivedFrom":makeQuery(id+"F2.opPattern","COPY",BODY,{"derivedFrom":makeQuery(id+"F1.opRevolve","SWEPT_BODY",BODY,{"disambiguationData":[OSD([sQuery(id+"F0.wireOp",EDGE,"E1")])]}),"instanceName":"1"}),"instanceName":"1"}),"instanceName":"1"}),"instanceName":"1"}),"instanceName":"1"}),"instanceName":"1"}),"instanceName":"1"});
            var Q356;
            Q356=makeQuery(id+"F10.opPattern","COPY",BODY,{"derivedFrom":makeQuery(id+"F9.opPattern","COPY",BODY,{"derivedFrom":makeQuery(id+"F8.opPattern","COPY",BODY,{"derivedFrom":makeQuery(id+"F6.opPattern","COPY",BODY,{"derivedFrom":makeQuery(id+"F5.opPattern","COPY",BODY,{"derivedFrom":makeQuery(id+"F4.opPattern","COPY",BODY,{"derivedFrom":makeQuery(id+"F1.opRevolve","SWEPT_BODY",BODY,{"disambiguationData":[OSD([sQuery(id+"F0.wireOp",EDGE,"E1")])]}),"instanceName":"1"}),"instanceName":"1"}),"instanceName":"1"}),"instanceName":"1"}),"instanceName":"1"}),"instanceName":"1"});
            var Q357;
            Q357=makeQuery(id+"F10.opPattern","COPY",BODY,{"derivedFrom":makeQuery(id+"F9.opPattern","COPY",BODY,{"derivedFrom":makeQuery(id+"F8.opPattern","COPY",BODY,{"derivedFrom":makeQuery(id+"F6.opPattern","COPY",BODY,{"derivedFrom":makeQuery(id+"F5.opPattern","COPY",BODY,{"derivedFrom":makeQuery(id+"F4.opPattern","COPY",BODY,{"derivedFrom":makeQuery(id+"F2.opPattern","COPY",BODY,{"derivedFrom":makeQuery(id+"F1.opRevolve","SWEPT_BODY",BODY,{"disambiguationData":[OSD([sQuery(id+"F0.wireOp",EDGE,"E1")])]}),"instanceName":"1"}),"instanceName":"1"}),"instanceName":"1"}),"instanceName":"1"}),"instanceName":"1"}),"instanceName":"1"}),"instanceName":"1"});
            var Q358;
            Q358=makeQuery(id+"F10.opPattern","COPY",BODY,{"derivedFrom":makeQuery(id+"F9.opPattern","COPY",BODY,{"derivedFrom":makeQuery(id+"F8.opPattern","COPY",BODY,{"derivedFrom":makeQuery(id+"F6.opPattern","COPY",BODY,{"derivedFrom":makeQuery(id+"F5.opPattern","COPY",BODY,{"derivedFrom":makeQuery(id+"F4.opPattern","COPY",BODY,{"derivedFrom":makeQuery(id+"F3.opPattern","COPY",BODY,{"derivedFrom":makeQuery(id+"F2.opPattern","COPY",BODY,{"derivedFrom":makeQuery(id+"F1.opRevolve","SWEPT_BODY",BODY,{"disambiguationData":[OSD([sQuery(id+"F0.wireOp",EDGE,"E1")])]}),"instanceName":"1"}),"instanceName":"1"}),"instanceName":"1"}),"instanceName":"1"}),"instanceName":"1"}),"instanceName":"1"}),"instanceName":"1"}),"instanceName":"1"});
            var Q359;
            Q359=makeQuery(id+"F10.opPattern","COPY",BODY,{"derivedFrom":makeQuery(id+"F9.opPattern","COPY",BODY,{"derivedFrom":makeQuery(id+"F8.opPattern","COPY",BODY,{"derivedFrom":makeQuery(id+"F7.opPattern","COPY",BODY,{"derivedFrom":makeQuery(id+"F1.opRevolve","SWEPT_BODY",BODY,{"disambiguationData":[OSD([sQuery(id+"F0.wireOp",EDGE,"E1")])]}),"instanceName":"1"}),"instanceName":"1"}),"instanceName":"1"}),"instanceName":"1"});
            var Q360;
            Q360=makeQuery(id+"F10.opPattern","COPY",BODY,{"derivedFrom":makeQuery(id+"F9.opPattern","COPY",BODY,{"derivedFrom":makeQuery(id+"F8.opPattern","COPY",BODY,{"derivedFrom":makeQuery(id+"F7.opPattern","COPY",BODY,{"derivedFrom":makeQuery(id+"F2.opPattern","COPY",BODY,{"derivedFrom":makeQuery(id+"F1.opRevolve","SWEPT_BODY",BODY,{"disambiguationData":[OSD([sQuery(id+"F0.wireOp",EDGE,"E1")])]}),"instanceName":"1"}),"instanceName":"1"}),"instanceName":"1"}),"instanceName":"1"}),"instanceName":"1"});
            var Q361;
            Q361=makeQuery(id+"F10.opPattern","COPY",BODY,{"derivedFrom":makeQuery(id+"F9.opPattern","COPY",BODY,{"derivedFrom":makeQuery(id+"F8.opPattern","COPY",BODY,{"derivedFrom":makeQuery(id+"F7.opPattern","COPY",BODY,{"derivedFrom":makeQuery(id+"F3.opPattern","COPY",BODY,{"derivedFrom":makeQuery(id+"F2.opPattern","COPY",BODY,{"derivedFrom":makeQuery(id+"F1.opRevolve","SWEPT_BODY",BODY,{"disambiguationData":[OSD([sQuery(id+"F0.wireOp",EDGE,"E1")])]}),"instanceName":"1"}),"instanceName":"1"}),"instanceName":"1"}),"instanceName":"1"}),"instanceName":"1"}),"instanceName":"1"});
            var Q362;
            Q362=makeQuery(id+"F10.opPattern","COPY",BODY,{"derivedFrom":makeQuery(id+"F9.opPattern","COPY",BODY,{"derivedFrom":makeQuery(id+"F8.opPattern","COPY",BODY,{"derivedFrom":makeQuery(id+"F7.opPattern","COPY",BODY,{"derivedFrom":makeQuery(id+"F4.opPattern","COPY",BODY,{"derivedFrom":makeQuery(id+"F1.opRevolve","SWEPT_BODY",BODY,{"disambiguationData":[OSD([sQuery(id+"F0.wireOp",EDGE,"E1")])]}),"instanceName":"1"}),"instanceName":"1"}),"instanceName":"1"}),"instanceName":"1"}),"instanceName":"1"});
            var Q363;
            Q363=makeQuery(id+"F10.opPattern","COPY",BODY,{"derivedFrom":makeQuery(id+"F9.opPattern","COPY",BODY,{"derivedFrom":makeQuery(id+"F8.opPattern","COPY",BODY,{"derivedFrom":makeQuery(id+"F7.opPattern","COPY",BODY,{"derivedFrom":makeQuery(id+"F4.opPattern","COPY",BODY,{"derivedFrom":makeQuery(id+"F2.opPattern","COPY",BODY,{"derivedFrom":makeQuery(id+"F1.opRevolve","SWEPT_BODY",BODY,{"disambiguationData":[OSD([sQuery(id+"F0.wireOp",EDGE,"E1")])]}),"instanceName":"1"}),"instanceName":"1"}),"instanceName":"1"}),"instanceName":"1"}),"instanceName":"1"}),"instanceName":"1"});
            var Q364;
            Q364=makeQuery(id+"F10.opPattern","COPY",BODY,{"derivedFrom":makeQuery(id+"F9.opPattern","COPY",BODY,{"derivedFrom":makeQuery(id+"F8.opPattern","COPY",BODY,{"derivedFrom":makeQuery(id+"F7.opPattern","COPY",BODY,{"derivedFrom":makeQuery(id+"F4.opPattern","COPY",BODY,{"derivedFrom":makeQuery(id+"F3.opPattern","COPY",BODY,{"derivedFrom":makeQuery(id+"F2.opPattern","COPY",BODY,{"derivedFrom":makeQuery(id+"F1.opRevolve","SWEPT_BODY",BODY,{"disambiguationData":[OSD([sQuery(id+"F0.wireOp",EDGE,"E1")])]}),"instanceName":"1"}),"instanceName":"1"}),"instanceName":"1"}),"instanceName":"1"}),"instanceName":"1"}),"instanceName":"1"}),"instanceName":"1"});
            var Q365;
            Q365=makeQuery(id+"F10.opPattern","COPY",BODY,{"derivedFrom":makeQuery(id+"F9.opPattern","COPY",BODY,{"derivedFrom":makeQuery(id+"F8.opPattern","COPY",BODY,{"derivedFrom":makeQuery(id+"F7.opPattern","COPY",BODY,{"derivedFrom":makeQuery(id+"F5.opPattern","COPY",BODY,{"derivedFrom":makeQuery(id+"F1.opRevolve","SWEPT_BODY",BODY,{"disambiguationData":[OSD([sQuery(id+"F0.wireOp",EDGE,"E1")])]}),"instanceName":"1"}),"instanceName":"1"}),"instanceName":"1"}),"instanceName":"1"}),"instanceName":"1"});
            var Q366;
            Q366=makeQuery(id+"F10.opPattern","COPY",BODY,{"derivedFrom":makeQuery(id+"F9.opPattern","COPY",BODY,{"derivedFrom":makeQuery(id+"F8.opPattern","COPY",BODY,{"derivedFrom":makeQuery(id+"F7.opPattern","COPY",BODY,{"derivedFrom":makeQuery(id+"F5.opPattern","COPY",BODY,{"derivedFrom":makeQuery(id+"F2.opPattern","COPY",BODY,{"derivedFrom":makeQuery(id+"F1.opRevolve","SWEPT_BODY",BODY,{"disambiguationData":[OSD([sQuery(id+"F0.wireOp",EDGE,"E1")])]}),"instanceName":"1"}),"instanceName":"1"}),"instanceName":"1"}),"instanceName":"1"}),"instanceName":"1"}),"instanceName":"1"});
            var Q367;
            Q367=makeQuery(id+"F10.opPattern","COPY",BODY,{"derivedFrom":makeQuery(id+"F9.opPattern","COPY",BODY,{"derivedFrom":makeQuery(id+"F8.opPattern","COPY",BODY,{"derivedFrom":makeQuery(id+"F7.opPattern","COPY",BODY,{"derivedFrom":makeQuery(id+"F5.opPattern","COPY",BODY,{"derivedFrom":makeQuery(id+"F3.opPattern","COPY",BODY,{"derivedFrom":makeQuery(id+"F2.opPattern","COPY",BODY,{"derivedFrom":makeQuery(id+"F1.opRevolve","SWEPT_BODY",BODY,{"disambiguationData":[OSD([sQuery(id+"F0.wireOp",EDGE,"E1")])]}),"instanceName":"1"}),"instanceName":"1"}),"instanceName":"1"}),"instanceName":"1"}),"instanceName":"1"}),"instanceName":"1"}),"instanceName":"1"});
            var Q368;
            Q368=makeQuery(id+"F10.opPattern","COPY",BODY,{"derivedFrom":makeQuery(id+"F9.opPattern","COPY",BODY,{"derivedFrom":makeQuery(id+"F8.opPattern","COPY",BODY,{"derivedFrom":makeQuery(id+"F7.opPattern","COPY",BODY,{"derivedFrom":makeQuery(id+"F5.opPattern","COPY",BODY,{"derivedFrom":makeQuery(id+"F4.opPattern","COPY",BODY,{"derivedFrom":makeQuery(id+"F1.opRevolve","SWEPT_BODY",BODY,{"disambiguationData":[OSD([sQuery(id+"F0.wireOp",EDGE,"E1")])]}),"instanceName":"1"}),"instanceName":"1"}),"instanceName":"1"}),"instanceName":"1"}),"instanceName":"1"}),"instanceName":"1"});
            var Q369;
            Q369=makeQuery(id+"F10.opPattern","COPY",BODY,{"derivedFrom":makeQuery(id+"F9.opPattern","COPY",BODY,{"derivedFrom":makeQuery(id+"F8.opPattern","COPY",BODY,{"derivedFrom":makeQuery(id+"F7.opPattern","COPY",BODY,{"derivedFrom":makeQuery(id+"F5.opPattern","COPY",BODY,{"derivedFrom":makeQuery(id+"F4.opPattern","COPY",BODY,{"derivedFrom":makeQuery(id+"F2.opPattern","COPY",BODY,{"derivedFrom":makeQuery(id+"F1.opRevolve","SWEPT_BODY",BODY,{"disambiguationData":[OSD([sQuery(id+"F0.wireOp",EDGE,"E1")])]}),"instanceName":"1"}),"instanceName":"1"}),"instanceName":"1"}),"instanceName":"1"}),"instanceName":"1"}),"instanceName":"1"}),"instanceName":"1"});
            var Q370;
            Q370=makeQuery(id+"F10.opPattern","COPY",BODY,{"derivedFrom":makeQuery(id+"F9.opPattern","COPY",BODY,{"derivedFrom":makeQuery(id+"F8.opPattern","COPY",BODY,{"derivedFrom":makeQuery(id+"F7.opPattern","COPY",BODY,{"derivedFrom":makeQuery(id+"F5.opPattern","COPY",BODY,{"derivedFrom":makeQuery(id+"F4.opPattern","COPY",BODY,{"derivedFrom":makeQuery(id+"F3.opPattern","COPY",BODY,{"derivedFrom":makeQuery(id+"F2.opPattern","COPY",BODY,{"derivedFrom":makeQuery(id+"F1.opRevolve","SWEPT_BODY",BODY,{"disambiguationData":[OSD([sQuery(id+"F0.wireOp",EDGE,"E1")])]}),"instanceName":"1"}),"instanceName":"1"}),"instanceName":"1"}),"instanceName":"1"}),"instanceName":"1"}),"instanceName":"1"}),"instanceName":"1"}),"instanceName":"1"});
            var Q371;
            Q371=makeQuery(id+"F10.opPattern","COPY",BODY,{"derivedFrom":makeQuery(id+"F9.opPattern","COPY",BODY,{"derivedFrom":makeQuery(id+"F8.opPattern","COPY",BODY,{"derivedFrom":makeQuery(id+"F7.opPattern","COPY",BODY,{"derivedFrom":makeQuery(id+"F6.opPattern","COPY",BODY,{"derivedFrom":makeQuery(id+"F1.opRevolve","SWEPT_BODY",BODY,{"disambiguationData":[OSD([sQuery(id+"F0.wireOp",EDGE,"E1")])]}),"instanceName":"1"}),"instanceName":"1"}),"instanceName":"1"}),"instanceName":"1"}),"instanceName":"1"});
            var Q372;
            Q372=makeQuery(id+"F10.opPattern","COPY",BODY,{"derivedFrom":makeQuery(id+"F9.opPattern","COPY",BODY,{"derivedFrom":makeQuery(id+"F8.opPattern","COPY",BODY,{"derivedFrom":makeQuery(id+"F7.opPattern","COPY",BODY,{"derivedFrom":makeQuery(id+"F6.opPattern","COPY",BODY,{"derivedFrom":makeQuery(id+"F2.opPattern","COPY",BODY,{"derivedFrom":makeQuery(id+"F1.opRevolve","SWEPT_BODY",BODY,{"disambiguationData":[OSD([sQuery(id+"F0.wireOp",EDGE,"E1")])]}),"instanceName":"1"}),"instanceName":"1"}),"instanceName":"1"}),"instanceName":"1"}),"instanceName":"1"}),"instanceName":"1"});
            var Q373;
            Q373=makeQuery(id+"F10.opPattern","COPY",BODY,{"derivedFrom":makeQuery(id+"F9.opPattern","COPY",BODY,{"derivedFrom":makeQuery(id+"F8.opPattern","COPY",BODY,{"derivedFrom":makeQuery(id+"F7.opPattern","COPY",BODY,{"derivedFrom":makeQuery(id+"F6.opPattern","COPY",BODY,{"derivedFrom":makeQuery(id+"F3.opPattern","COPY",BODY,{"derivedFrom":makeQuery(id+"F2.opPattern","COPY",BODY,{"derivedFrom":makeQuery(id+"F1.opRevolve","SWEPT_BODY",BODY,{"disambiguationData":[OSD([sQuery(id+"F0.wireOp",EDGE,"E1")])]}),"instanceName":"1"}),"instanceName":"1"}),"instanceName":"1"}),"instanceName":"1"}),"instanceName":"1"}),"instanceName":"1"}),"instanceName":"1"});
            var Q374;
            Q374=makeQuery(id+"F10.opPattern","COPY",BODY,{"derivedFrom":makeQuery(id+"F9.opPattern","COPY",BODY,{"derivedFrom":makeQuery(id+"F8.opPattern","COPY",BODY,{"derivedFrom":makeQuery(id+"F7.opPattern","COPY",BODY,{"derivedFrom":makeQuery(id+"F6.opPattern","COPY",BODY,{"derivedFrom":makeQuery(id+"F4.opPattern","COPY",BODY,{"derivedFrom":makeQuery(id+"F1.opRevolve","SWEPT_BODY",BODY,{"disambiguationData":[OSD([sQuery(id+"F0.wireOp",EDGE,"E1")])]}),"instanceName":"1"}),"instanceName":"1"}),"instanceName":"1"}),"instanceName":"1"}),"instanceName":"1"}),"instanceName":"1"});
            var Q375;
            Q375=makeQuery(id+"F10.opPattern","COPY",BODY,{"derivedFrom":makeQuery(id+"F9.opPattern","COPY",BODY,{"derivedFrom":makeQuery(id+"F8.opPattern","COPY",BODY,{"derivedFrom":makeQuery(id+"F7.opPattern","COPY",BODY,{"derivedFrom":makeQuery(id+"F6.opPattern","COPY",BODY,{"derivedFrom":makeQuery(id+"F4.opPattern","COPY",BODY,{"derivedFrom":makeQuery(id+"F2.opPattern","COPY",BODY,{"derivedFrom":makeQuery(id+"F1.opRevolve","SWEPT_BODY",BODY,{"disambiguationData":[OSD([sQuery(id+"F0.wireOp",EDGE,"E1")])]}),"instanceName":"1"}),"instanceName":"1"}),"instanceName":"1"}),"instanceName":"1"}),"instanceName":"1"}),"instanceName":"1"}),"instanceName":"1"});
            var Q376;
            Q376=makeQuery(id+"F10.opPattern","COPY",BODY,{"derivedFrom":makeQuery(id+"F9.opPattern","COPY",BODY,{"derivedFrom":makeQuery(id+"F8.opPattern","COPY",BODY,{"derivedFrom":makeQuery(id+"F7.opPattern","COPY",BODY,{"derivedFrom":makeQuery(id+"F6.opPattern","COPY",BODY,{"derivedFrom":makeQuery(id+"F4.opPattern","COPY",BODY,{"derivedFrom":makeQuery(id+"F3.opPattern","COPY",BODY,{"derivedFrom":makeQuery(id+"F2.opPattern","COPY",BODY,{"derivedFrom":makeQuery(id+"F1.opRevolve","SWEPT_BODY",BODY,{"disambiguationData":[OSD([sQuery(id+"F0.wireOp",EDGE,"E1")])]}),"instanceName":"1"}),"instanceName":"1"}),"instanceName":"1"}),"instanceName":"1"}),"instanceName":"1"}),"instanceName":"1"}),"instanceName":"1"}),"instanceName":"1"});
            var Q377;
            Q377=makeQuery(id+"F10.opPattern","COPY",BODY,{"derivedFrom":makeQuery(id+"F9.opPattern","COPY",BODY,{"derivedFrom":makeQuery(id+"F8.opPattern","COPY",BODY,{"derivedFrom":makeQuery(id+"F7.opPattern","COPY",BODY,{"derivedFrom":makeQuery(id+"F6.opPattern","COPY",BODY,{"derivedFrom":makeQuery(id+"F5.opPattern","COPY",BODY,{"derivedFrom":makeQuery(id+"F1.opRevolve","SWEPT_BODY",BODY,{"disambiguationData":[OSD([sQuery(id+"F0.wireOp",EDGE,"E1")])]}),"instanceName":"1"}),"instanceName":"1"}),"instanceName":"1"}),"instanceName":"1"}),"instanceName":"1"}),"instanceName":"1"});
            var Q378;
            Q378=makeQuery(id+"F10.opPattern","COPY",BODY,{"derivedFrom":makeQuery(id+"F9.opPattern","COPY",BODY,{"derivedFrom":makeQuery(id+"F8.opPattern","COPY",BODY,{"derivedFrom":makeQuery(id+"F7.opPattern","COPY",BODY,{"derivedFrom":makeQuery(id+"F6.opPattern","COPY",BODY,{"derivedFrom":makeQuery(id+"F5.opPattern","COPY",BODY,{"derivedFrom":makeQuery(id+"F2.opPattern","COPY",BODY,{"derivedFrom":makeQuery(id+"F1.opRevolve","SWEPT_BODY",BODY,{"disambiguationData":[OSD([sQuery(id+"F0.wireOp",EDGE,"E1")])]}),"instanceName":"1"}),"instanceName":"1"}),"instanceName":"1"}),"instanceName":"1"}),"instanceName":"1"}),"instanceName":"1"}),"instanceName":"1"});
            var Q379;
            Q379=makeQuery(id+"F10.opPattern","COPY",BODY,{"derivedFrom":makeQuery(id+"F9.opPattern","COPY",BODY,{"derivedFrom":makeQuery(id+"F8.opPattern","COPY",BODY,{"derivedFrom":makeQuery(id+"F7.opPattern","COPY",BODY,{"derivedFrom":makeQuery(id+"F6.opPattern","COPY",BODY,{"derivedFrom":makeQuery(id+"F5.opPattern","COPY",BODY,{"derivedFrom":makeQuery(id+"F3.opPattern","COPY",BODY,{"derivedFrom":makeQuery(id+"F2.opPattern","COPY",BODY,{"derivedFrom":makeQuery(id+"F1.opRevolve","SWEPT_BODY",BODY,{"disambiguationData":[OSD([sQuery(id+"F0.wireOp",EDGE,"E1")])]}),"instanceName":"1"}),"instanceName":"1"}),"instanceName":"1"}),"instanceName":"1"}),"instanceName":"1"}),"instanceName":"1"}),"instanceName":"1"}),"instanceName":"1"});
            var Q380;
            Q380=makeQuery(id+"F10.opPattern","COPY",BODY,{"derivedFrom":makeQuery(id+"F9.opPattern","COPY",BODY,{"derivedFrom":makeQuery(id+"F8.opPattern","COPY",BODY,{"derivedFrom":makeQuery(id+"F7.opPattern","COPY",BODY,{"derivedFrom":makeQuery(id+"F6.opPattern","COPY",BODY,{"derivedFrom":makeQuery(id+"F5.opPattern","COPY",BODY,{"derivedFrom":makeQuery(id+"F4.opPattern","COPY",BODY,{"derivedFrom":makeQuery(id+"F1.opRevolve","SWEPT_BODY",BODY,{"disambiguationData":[OSD([sQuery(id+"F0.wireOp",EDGE,"E1")])]}),"instanceName":"1"}),"instanceName":"1"}),"instanceName":"1"}),"instanceName":"1"}),"instanceName":"1"}),"instanceName":"1"}),"instanceName":"1"});
            var Q381;
            Q381=makeQuery(id+"F10.opPattern","COPY",BODY,{"derivedFrom":makeQuery(id+"F9.opPattern","COPY",BODY,{"derivedFrom":makeQuery(id+"F8.opPattern","COPY",BODY,{"derivedFrom":makeQuery(id+"F7.opPattern","COPY",BODY,{"derivedFrom":makeQuery(id+"F6.opPattern","COPY",BODY,{"derivedFrom":makeQuery(id+"F5.opPattern","COPY",BODY,{"derivedFrom":makeQuery(id+"F4.opPattern","COPY",BODY,{"derivedFrom":makeQuery(id+"F2.opPattern","COPY",BODY,{"derivedFrom":makeQuery(id+"F1.opRevolve","SWEPT_BODY",BODY,{"disambiguationData":[OSD([sQuery(id+"F0.wireOp",EDGE,"E1")])]}),"instanceName":"1"}),"instanceName":"1"}),"instanceName":"1"}),"instanceName":"1"}),"instanceName":"1"}),"instanceName":"1"}),"instanceName":"1"}),"instanceName":"1"});
            var Q382;
            Q382=makeQuery(id+"F10.opPattern","COPY",BODY,{"derivedFrom":makeQuery(id+"F9.opPattern","COPY",BODY,{"derivedFrom":makeQuery(id+"F8.opPattern","COPY",BODY,{"derivedFrom":makeQuery(id+"F7.opPattern","COPY",BODY,{"derivedFrom":makeQuery(id+"F6.opPattern","COPY",BODY,{"derivedFrom":makeQuery(id+"F5.opPattern","COPY",BODY,{"derivedFrom":makeQuery(id+"F4.opPattern","COPY",BODY,{"derivedFrom":makeQuery(id+"F3.opPattern","COPY",BODY,{"derivedFrom":makeQuery(id+"F2.opPattern","COPY",BODY,{"derivedFrom":makeQuery(id+"F1.opRevolve","SWEPT_BODY",BODY,{"disambiguationData":[OSD([sQuery(id+"F0.wireOp",EDGE,"E1")])]}),"instanceName":"1"}),"instanceName":"1"}),"instanceName":"1"}),"instanceName":"1"}),"instanceName":"1"}),"instanceName":"1"}),"instanceName":"1"}),"instanceName":"1"}),"instanceName":"1"});
            var Q383;
            Q383=makeQuery(id+"F11.opPattern","COPY",BODY,{"derivedFrom":makeQuery(id+"F1.opRevolve","SWEPT_BODY",BODY,{"disambiguationData":[OSD([sQuery(id+"F0.wireOp",EDGE,"E1")])]}),"instanceName":"1"});
            var Q384;
            Q384=makeQuery(id+"F11.opPattern","COPY",BODY,{"derivedFrom":makeQuery(id+"F2.opPattern","COPY",BODY,{"derivedFrom":makeQuery(id+"F1.opRevolve","SWEPT_BODY",BODY,{"disambiguationData":[OSD([sQuery(id+"F0.wireOp",EDGE,"E1")])]}),"instanceName":"1"}),"instanceName":"1"});
            var Q385;
            Q385=makeQuery(id+"F11.opPattern","COPY",BODY,{"derivedFrom":makeQuery(id+"F3.opPattern","COPY",BODY,{"derivedFrom":makeQuery(id+"F2.opPattern","COPY",BODY,{"derivedFrom":makeQuery(id+"F1.opRevolve","SWEPT_BODY",BODY,{"disambiguationData":[OSD([sQuery(id+"F0.wireOp",EDGE,"E1")])]}),"instanceName":"1"}),"instanceName":"1"}),"instanceName":"1"});
            var Q386;
            Q386=makeQuery(id+"F11.opPattern","COPY",BODY,{"derivedFrom":makeQuery(id+"F4.opPattern","COPY",BODY,{"derivedFrom":makeQuery(id+"F1.opRevolve","SWEPT_BODY",BODY,{"disambiguationData":[OSD([sQuery(id+"F0.wireOp",EDGE,"E1")])]}),"instanceName":"1"}),"instanceName":"1"});
            var Q387;
            Q387=makeQuery(id+"F11.opPattern","COPY",BODY,{"derivedFrom":makeQuery(id+"F4.opPattern","COPY",BODY,{"derivedFrom":makeQuery(id+"F2.opPattern","COPY",BODY,{"derivedFrom":makeQuery(id+"F1.opRevolve","SWEPT_BODY",BODY,{"disambiguationData":[OSD([sQuery(id+"F0.wireOp",EDGE,"E1")])]}),"instanceName":"1"}),"instanceName":"1"}),"instanceName":"1"});
            var Q388;
            Q388=makeQuery(id+"F11.opPattern","COPY",BODY,{"derivedFrom":makeQuery(id+"F4.opPattern","COPY",BODY,{"derivedFrom":makeQuery(id+"F3.opPattern","COPY",BODY,{"derivedFrom":makeQuery(id+"F2.opPattern","COPY",BODY,{"derivedFrom":makeQuery(id+"F1.opRevolve","SWEPT_BODY",BODY,{"disambiguationData":[OSD([sQuery(id+"F0.wireOp",EDGE,"E1")])]}),"instanceName":"1"}),"instanceName":"1"}),"instanceName":"1"}),"instanceName":"1"});
            var Q389;
            Q389=makeQuery(id+"F11.opPattern","COPY",BODY,{"derivedFrom":makeQuery(id+"F5.opPattern","COPY",BODY,{"derivedFrom":makeQuery(id+"F1.opRevolve","SWEPT_BODY",BODY,{"disambiguationData":[OSD([sQuery(id+"F0.wireOp",EDGE,"E1")])]}),"instanceName":"1"}),"instanceName":"1"});
            var Q390;
            Q390=makeQuery(id+"F11.opPattern","COPY",BODY,{"derivedFrom":makeQuery(id+"F5.opPattern","COPY",BODY,{"derivedFrom":makeQuery(id+"F2.opPattern","COPY",BODY,{"derivedFrom":makeQuery(id+"F1.opRevolve","SWEPT_BODY",BODY,{"disambiguationData":[OSD([sQuery(id+"F0.wireOp",EDGE,"E1")])]}),"instanceName":"1"}),"instanceName":"1"}),"instanceName":"1"});
            var Q391;
            Q391=makeQuery(id+"F11.opPattern","COPY",BODY,{"derivedFrom":makeQuery(id+"F5.opPattern","COPY",BODY,{"derivedFrom":makeQuery(id+"F3.opPattern","COPY",BODY,{"derivedFrom":makeQuery(id+"F2.opPattern","COPY",BODY,{"derivedFrom":makeQuery(id+"F1.opRevolve","SWEPT_BODY",BODY,{"disambiguationData":[OSD([sQuery(id+"F0.wireOp",EDGE,"E1")])]}),"instanceName":"1"}),"instanceName":"1"}),"instanceName":"1"}),"instanceName":"1"});
            var Q392;
            Q392=makeQuery(id+"F11.opPattern","COPY",BODY,{"derivedFrom":makeQuery(id+"F5.opPattern","COPY",BODY,{"derivedFrom":makeQuery(id+"F4.opPattern","COPY",BODY,{"derivedFrom":makeQuery(id+"F1.opRevolve","SWEPT_BODY",BODY,{"disambiguationData":[OSD([sQuery(id+"F0.wireOp",EDGE,"E1")])]}),"instanceName":"1"}),"instanceName":"1"}),"instanceName":"1"});
            var Q393;
            Q393=makeQuery(id+"F11.opPattern","COPY",BODY,{"derivedFrom":makeQuery(id+"F5.opPattern","COPY",BODY,{"derivedFrom":makeQuery(id+"F4.opPattern","COPY",BODY,{"derivedFrom":makeQuery(id+"F2.opPattern","COPY",BODY,{"derivedFrom":makeQuery(id+"F1.opRevolve","SWEPT_BODY",BODY,{"disambiguationData":[OSD([sQuery(id+"F0.wireOp",EDGE,"E1")])]}),"instanceName":"1"}),"instanceName":"1"}),"instanceName":"1"}),"instanceName":"1"});
            var Q394;
            Q394=makeQuery(id+"F11.opPattern","COPY",BODY,{"derivedFrom":makeQuery(id+"F5.opPattern","COPY",BODY,{"derivedFrom":makeQuery(id+"F4.opPattern","COPY",BODY,{"derivedFrom":makeQuery(id+"F3.opPattern","COPY",BODY,{"derivedFrom":makeQuery(id+"F2.opPattern","COPY",BODY,{"derivedFrom":makeQuery(id+"F1.opRevolve","SWEPT_BODY",BODY,{"disambiguationData":[OSD([sQuery(id+"F0.wireOp",EDGE,"E1")])]}),"instanceName":"1"}),"instanceName":"1"}),"instanceName":"1"}),"instanceName":"1"}),"instanceName":"1"});
            var Q395;
            Q395=makeQuery(id+"F11.opPattern","COPY",BODY,{"derivedFrom":makeQuery(id+"F6.opPattern","COPY",BODY,{"derivedFrom":makeQuery(id+"F1.opRevolve","SWEPT_BODY",BODY,{"disambiguationData":[OSD([sQuery(id+"F0.wireOp",EDGE,"E1")])]}),"instanceName":"1"}),"instanceName":"1"});
            var Q396;
            Q396=makeQuery(id+"F11.opPattern","COPY",BODY,{"derivedFrom":makeQuery(id+"F6.opPattern","COPY",BODY,{"derivedFrom":makeQuery(id+"F2.opPattern","COPY",BODY,{"derivedFrom":makeQuery(id+"F1.opRevolve","SWEPT_BODY",BODY,{"disambiguationData":[OSD([sQuery(id+"F0.wireOp",EDGE,"E1")])]}),"instanceName":"1"}),"instanceName":"1"}),"instanceName":"1"});
            var Q397;
            Q397=makeQuery(id+"F11.opPattern","COPY",BODY,{"derivedFrom":makeQuery(id+"F6.opPattern","COPY",BODY,{"derivedFrom":makeQuery(id+"F3.opPattern","COPY",BODY,{"derivedFrom":makeQuery(id+"F2.opPattern","COPY",BODY,{"derivedFrom":makeQuery(id+"F1.opRevolve","SWEPT_BODY",BODY,{"disambiguationData":[OSD([sQuery(id+"F0.wireOp",EDGE,"E1")])]}),"instanceName":"1"}),"instanceName":"1"}),"instanceName":"1"}),"instanceName":"1"});
            var Q398;
            Q398=makeQuery(id+"F11.opPattern","COPY",BODY,{"derivedFrom":makeQuery(id+"F6.opPattern","COPY",BODY,{"derivedFrom":makeQuery(id+"F4.opPattern","COPY",BODY,{"derivedFrom":makeQuery(id+"F1.opRevolve","SWEPT_BODY",BODY,{"disambiguationData":[OSD([sQuery(id+"F0.wireOp",EDGE,"E1")])]}),"instanceName":"1"}),"instanceName":"1"}),"instanceName":"1"});
            var Q399;
            Q399=makeQuery(id+"F11.opPattern","COPY",BODY,{"derivedFrom":makeQuery(id+"F6.opPattern","COPY",BODY,{"derivedFrom":makeQuery(id+"F4.opPattern","COPY",BODY,{"derivedFrom":makeQuery(id+"F2.opPattern","COPY",BODY,{"derivedFrom":makeQuery(id+"F1.opRevolve","SWEPT_BODY",BODY,{"disambiguationData":[OSD([sQuery(id+"F0.wireOp",EDGE,"E1")])]}),"instanceName":"1"}),"instanceName":"1"}),"instanceName":"1"}),"instanceName":"1"});
            var Q400;
            Q400=makeQuery(id+"F11.opPattern","COPY",BODY,{"derivedFrom":makeQuery(id+"F6.opPattern","COPY",BODY,{"derivedFrom":makeQuery(id+"F4.opPattern","COPY",BODY,{"derivedFrom":makeQuery(id+"F3.opPattern","COPY",BODY,{"derivedFrom":makeQuery(id+"F2.opPattern","COPY",BODY,{"derivedFrom":makeQuery(id+"F1.opRevolve","SWEPT_BODY",BODY,{"disambiguationData":[OSD([sQuery(id+"F0.wireOp",EDGE,"E1")])]}),"instanceName":"1"}),"instanceName":"1"}),"instanceName":"1"}),"instanceName":"1"}),"instanceName":"1"});
            var Q401;
            Q401=makeQuery(id+"F11.opPattern","COPY",BODY,{"derivedFrom":makeQuery(id+"F6.opPattern","COPY",BODY,{"derivedFrom":makeQuery(id+"F5.opPattern","COPY",BODY,{"derivedFrom":makeQuery(id+"F1.opRevolve","SWEPT_BODY",BODY,{"disambiguationData":[OSD([sQuery(id+"F0.wireOp",EDGE,"E1")])]}),"instanceName":"1"}),"instanceName":"1"}),"instanceName":"1"});
            var Q402;
            Q402=makeQuery(id+"F11.opPattern","COPY",BODY,{"derivedFrom":makeQuery(id+"F6.opPattern","COPY",BODY,{"derivedFrom":makeQuery(id+"F5.opPattern","COPY",BODY,{"derivedFrom":makeQuery(id+"F2.opPattern","COPY",BODY,{"derivedFrom":makeQuery(id+"F1.opRevolve","SWEPT_BODY",BODY,{"disambiguationData":[OSD([sQuery(id+"F0.wireOp",EDGE,"E1")])]}),"instanceName":"1"}),"instanceName":"1"}),"instanceName":"1"}),"instanceName":"1"});
            var Q403;
            Q403=makeQuery(id+"F11.opPattern","COPY",BODY,{"derivedFrom":makeQuery(id+"F6.opPattern","COPY",BODY,{"derivedFrom":makeQuery(id+"F5.opPattern","COPY",BODY,{"derivedFrom":makeQuery(id+"F3.opPattern","COPY",BODY,{"derivedFrom":makeQuery(id+"F2.opPattern","COPY",BODY,{"derivedFrom":makeQuery(id+"F1.opRevolve","SWEPT_BODY",BODY,{"disambiguationData":[OSD([sQuery(id+"F0.wireOp",EDGE,"E1")])]}),"instanceName":"1"}),"instanceName":"1"}),"instanceName":"1"}),"instanceName":"1"}),"instanceName":"1"});
            var Q404;
            Q404=makeQuery(id+"F11.opPattern","COPY",BODY,{"derivedFrom":makeQuery(id+"F6.opPattern","COPY",BODY,{"derivedFrom":makeQuery(id+"F5.opPattern","COPY",BODY,{"derivedFrom":makeQuery(id+"F4.opPattern","COPY",BODY,{"derivedFrom":makeQuery(id+"F1.opRevolve","SWEPT_BODY",BODY,{"disambiguationData":[OSD([sQuery(id+"F0.wireOp",EDGE,"E1")])]}),"instanceName":"1"}),"instanceName":"1"}),"instanceName":"1"}),"instanceName":"1"});
            var Q405;
            Q405=makeQuery(id+"F11.opPattern","COPY",BODY,{"derivedFrom":makeQuery(id+"F6.opPattern","COPY",BODY,{"derivedFrom":makeQuery(id+"F5.opPattern","COPY",BODY,{"derivedFrom":makeQuery(id+"F4.opPattern","COPY",BODY,{"derivedFrom":makeQuery(id+"F2.opPattern","COPY",BODY,{"derivedFrom":makeQuery(id+"F1.opRevolve","SWEPT_BODY",BODY,{"disambiguationData":[OSD([sQuery(id+"F0.wireOp",EDGE,"E1")])]}),"instanceName":"1"}),"instanceName":"1"}),"instanceName":"1"}),"instanceName":"1"}),"instanceName":"1"});
            var Q406;
            Q406=makeQuery(id+"F11.opPattern","COPY",BODY,{"derivedFrom":makeQuery(id+"F6.opPattern","COPY",BODY,{"derivedFrom":makeQuery(id+"F5.opPattern","COPY",BODY,{"derivedFrom":makeQuery(id+"F4.opPattern","COPY",BODY,{"derivedFrom":makeQuery(id+"F3.opPattern","COPY",BODY,{"derivedFrom":makeQuery(id+"F2.opPattern","COPY",BODY,{"derivedFrom":makeQuery(id+"F1.opRevolve","SWEPT_BODY",BODY,{"disambiguationData":[OSD([sQuery(id+"F0.wireOp",EDGE,"E1")])]}),"instanceName":"1"}),"instanceName":"1"}),"instanceName":"1"}),"instanceName":"1"}),"instanceName":"1"}),"instanceName":"1"});
            var Q407;
            Q407=makeQuery(id+"F11.opPattern","COPY",BODY,{"derivedFrom":makeQuery(id+"F7.opPattern","COPY",BODY,{"derivedFrom":makeQuery(id+"F1.opRevolve","SWEPT_BODY",BODY,{"disambiguationData":[OSD([sQuery(id+"F0.wireOp",EDGE,"E1")])]}),"instanceName":"1"}),"instanceName":"1"});
            var Q408;
            Q408=makeQuery(id+"F11.opPattern","COPY",BODY,{"derivedFrom":makeQuery(id+"F7.opPattern","COPY",BODY,{"derivedFrom":makeQuery(id+"F2.opPattern","COPY",BODY,{"derivedFrom":makeQuery(id+"F1.opRevolve","SWEPT_BODY",BODY,{"disambiguationData":[OSD([sQuery(id+"F0.wireOp",EDGE,"E1")])]}),"instanceName":"1"}),"instanceName":"1"}),"instanceName":"1"});
            var Q409;
            Q409=makeQuery(id+"F11.opPattern","COPY",BODY,{"derivedFrom":makeQuery(id+"F7.opPattern","COPY",BODY,{"derivedFrom":makeQuery(id+"F3.opPattern","COPY",BODY,{"derivedFrom":makeQuery(id+"F2.opPattern","COPY",BODY,{"derivedFrom":makeQuery(id+"F1.opRevolve","SWEPT_BODY",BODY,{"disambiguationData":[OSD([sQuery(id+"F0.wireOp",EDGE,"E1")])]}),"instanceName":"1"}),"instanceName":"1"}),"instanceName":"1"}),"instanceName":"1"});
            var Q410;
            Q410=makeQuery(id+"F11.opPattern","COPY",BODY,{"derivedFrom":makeQuery(id+"F7.opPattern","COPY",BODY,{"derivedFrom":makeQuery(id+"F4.opPattern","COPY",BODY,{"derivedFrom":makeQuery(id+"F1.opRevolve","SWEPT_BODY",BODY,{"disambiguationData":[OSD([sQuery(id+"F0.wireOp",EDGE,"E1")])]}),"instanceName":"1"}),"instanceName":"1"}),"instanceName":"1"});
            var Q411;
            Q411=makeQuery(id+"F11.opPattern","COPY",BODY,{"derivedFrom":makeQuery(id+"F7.opPattern","COPY",BODY,{"derivedFrom":makeQuery(id+"F4.opPattern","COPY",BODY,{"derivedFrom":makeQuery(id+"F2.opPattern","COPY",BODY,{"derivedFrom":makeQuery(id+"F1.opRevolve","SWEPT_BODY",BODY,{"disambiguationData":[OSD([sQuery(id+"F0.wireOp",EDGE,"E1")])]}),"instanceName":"1"}),"instanceName":"1"}),"instanceName":"1"}),"instanceName":"1"});
            var Q412;
            Q412=makeQuery(id+"F11.opPattern","COPY",BODY,{"derivedFrom":makeQuery(id+"F7.opPattern","COPY",BODY,{"derivedFrom":makeQuery(id+"F4.opPattern","COPY",BODY,{"derivedFrom":makeQuery(id+"F3.opPattern","COPY",BODY,{"derivedFrom":makeQuery(id+"F2.opPattern","COPY",BODY,{"derivedFrom":makeQuery(id+"F1.opRevolve","SWEPT_BODY",BODY,{"disambiguationData":[OSD([sQuery(id+"F0.wireOp",EDGE,"E1")])]}),"instanceName":"1"}),"instanceName":"1"}),"instanceName":"1"}),"instanceName":"1"}),"instanceName":"1"});
            var Q413;
            Q413=makeQuery(id+"F11.opPattern","COPY",BODY,{"derivedFrom":makeQuery(id+"F7.opPattern","COPY",BODY,{"derivedFrom":makeQuery(id+"F5.opPattern","COPY",BODY,{"derivedFrom":makeQuery(id+"F1.opRevolve","SWEPT_BODY",BODY,{"disambiguationData":[OSD([sQuery(id+"F0.wireOp",EDGE,"E1")])]}),"instanceName":"1"}),"instanceName":"1"}),"instanceName":"1"});
            var Q414;
            Q414=makeQuery(id+"F11.opPattern","COPY",BODY,{"derivedFrom":makeQuery(id+"F7.opPattern","COPY",BODY,{"derivedFrom":makeQuery(id+"F5.opPattern","COPY",BODY,{"derivedFrom":makeQuery(id+"F2.opPattern","COPY",BODY,{"derivedFrom":makeQuery(id+"F1.opRevolve","SWEPT_BODY",BODY,{"disambiguationData":[OSD([sQuery(id+"F0.wireOp",EDGE,"E1")])]}),"instanceName":"1"}),"instanceName":"1"}),"instanceName":"1"}),"instanceName":"1"});
            var Q415;
            Q415=makeQuery(id+"F11.opPattern","COPY",BODY,{"derivedFrom":makeQuery(id+"F7.opPattern","COPY",BODY,{"derivedFrom":makeQuery(id+"F5.opPattern","COPY",BODY,{"derivedFrom":makeQuery(id+"F3.opPattern","COPY",BODY,{"derivedFrom":makeQuery(id+"F2.opPattern","COPY",BODY,{"derivedFrom":makeQuery(id+"F1.opRevolve","SWEPT_BODY",BODY,{"disambiguationData":[OSD([sQuery(id+"F0.wireOp",EDGE,"E1")])]}),"instanceName":"1"}),"instanceName":"1"}),"instanceName":"1"}),"instanceName":"1"}),"instanceName":"1"});
            var Q416;
            Q416=makeQuery(id+"F11.opPattern","COPY",BODY,{"derivedFrom":makeQuery(id+"F7.opPattern","COPY",BODY,{"derivedFrom":makeQuery(id+"F5.opPattern","COPY",BODY,{"derivedFrom":makeQuery(id+"F4.opPattern","COPY",BODY,{"derivedFrom":makeQuery(id+"F1.opRevolve","SWEPT_BODY",BODY,{"disambiguationData":[OSD([sQuery(id+"F0.wireOp",EDGE,"E1")])]}),"instanceName":"1"}),"instanceName":"1"}),"instanceName":"1"}),"instanceName":"1"});
            var Q417;
            Q417=makeQuery(id+"F11.opPattern","COPY",BODY,{"derivedFrom":makeQuery(id+"F7.opPattern","COPY",BODY,{"derivedFrom":makeQuery(id+"F5.opPattern","COPY",BODY,{"derivedFrom":makeQuery(id+"F4.opPattern","COPY",BODY,{"derivedFrom":makeQuery(id+"F2.opPattern","COPY",BODY,{"derivedFrom":makeQuery(id+"F1.opRevolve","SWEPT_BODY",BODY,{"disambiguationData":[OSD([sQuery(id+"F0.wireOp",EDGE,"E1")])]}),"instanceName":"1"}),"instanceName":"1"}),"instanceName":"1"}),"instanceName":"1"}),"instanceName":"1"});
            var Q418;
            Q418=makeQuery(id+"F11.opPattern","COPY",BODY,{"derivedFrom":makeQuery(id+"F7.opPattern","COPY",BODY,{"derivedFrom":makeQuery(id+"F5.opPattern","COPY",BODY,{"derivedFrom":makeQuery(id+"F4.opPattern","COPY",BODY,{"derivedFrom":makeQuery(id+"F3.opPattern","COPY",BODY,{"derivedFrom":makeQuery(id+"F2.opPattern","COPY",BODY,{"derivedFrom":makeQuery(id+"F1.opRevolve","SWEPT_BODY",BODY,{"disambiguationData":[OSD([sQuery(id+"F0.wireOp",EDGE,"E1")])]}),"instanceName":"1"}),"instanceName":"1"}),"instanceName":"1"}),"instanceName":"1"}),"instanceName":"1"}),"instanceName":"1"});
            var Q419;
            Q419=makeQuery(id+"F11.opPattern","COPY",BODY,{"derivedFrom":makeQuery(id+"F7.opPattern","COPY",BODY,{"derivedFrom":makeQuery(id+"F6.opPattern","COPY",BODY,{"derivedFrom":makeQuery(id+"F1.opRevolve","SWEPT_BODY",BODY,{"disambiguationData":[OSD([sQuery(id+"F0.wireOp",EDGE,"E1")])]}),"instanceName":"1"}),"instanceName":"1"}),"instanceName":"1"});
            var Q420;
            Q420=makeQuery(id+"F11.opPattern","COPY",BODY,{"derivedFrom":makeQuery(id+"F7.opPattern","COPY",BODY,{"derivedFrom":makeQuery(id+"F6.opPattern","COPY",BODY,{"derivedFrom":makeQuery(id+"F2.opPattern","COPY",BODY,{"derivedFrom":makeQuery(id+"F1.opRevolve","SWEPT_BODY",BODY,{"disambiguationData":[OSD([sQuery(id+"F0.wireOp",EDGE,"E1")])]}),"instanceName":"1"}),"instanceName":"1"}),"instanceName":"1"}),"instanceName":"1"});
            var Q421;
            Q421=makeQuery(id+"F11.opPattern","COPY",BODY,{"derivedFrom":makeQuery(id+"F7.opPattern","COPY",BODY,{"derivedFrom":makeQuery(id+"F6.opPattern","COPY",BODY,{"derivedFrom":makeQuery(id+"F3.opPattern","COPY",BODY,{"derivedFrom":makeQuery(id+"F2.opPattern","COPY",BODY,{"derivedFrom":makeQuery(id+"F1.opRevolve","SWEPT_BODY",BODY,{"disambiguationData":[OSD([sQuery(id+"F0.wireOp",EDGE,"E1")])]}),"instanceName":"1"}),"instanceName":"1"}),"instanceName":"1"}),"instanceName":"1"}),"instanceName":"1"});
            var Q422;
            Q422=makeQuery(id+"F11.opPattern","COPY",BODY,{"derivedFrom":makeQuery(id+"F7.opPattern","COPY",BODY,{"derivedFrom":makeQuery(id+"F6.opPattern","COPY",BODY,{"derivedFrom":makeQuery(id+"F4.opPattern","COPY",BODY,{"derivedFrom":makeQuery(id+"F1.opRevolve","SWEPT_BODY",BODY,{"disambiguationData":[OSD([sQuery(id+"F0.wireOp",EDGE,"E1")])]}),"instanceName":"1"}),"instanceName":"1"}),"instanceName":"1"}),"instanceName":"1"});
            var Q423;
            Q423=makeQuery(id+"F11.opPattern","COPY",BODY,{"derivedFrom":makeQuery(id+"F7.opPattern","COPY",BODY,{"derivedFrom":makeQuery(id+"F6.opPattern","COPY",BODY,{"derivedFrom":makeQuery(id+"F4.opPattern","COPY",BODY,{"derivedFrom":makeQuery(id+"F2.opPattern","COPY",BODY,{"derivedFrom":makeQuery(id+"F1.opRevolve","SWEPT_BODY",BODY,{"disambiguationData":[OSD([sQuery(id+"F0.wireOp",EDGE,"E1")])]}),"instanceName":"1"}),"instanceName":"1"}),"instanceName":"1"}),"instanceName":"1"}),"instanceName":"1"});
            var Q424;
            Q424=makeQuery(id+"F11.opPattern","COPY",BODY,{"derivedFrom":makeQuery(id+"F7.opPattern","COPY",BODY,{"derivedFrom":makeQuery(id+"F6.opPattern","COPY",BODY,{"derivedFrom":makeQuery(id+"F4.opPattern","COPY",BODY,{"derivedFrom":makeQuery(id+"F3.opPattern","COPY",BODY,{"derivedFrom":makeQuery(id+"F2.opPattern","COPY",BODY,{"derivedFrom":makeQuery(id+"F1.opRevolve","SWEPT_BODY",BODY,{"disambiguationData":[OSD([sQuery(id+"F0.wireOp",EDGE,"E1")])]}),"instanceName":"1"}),"instanceName":"1"}),"instanceName":"1"}),"instanceName":"1"}),"instanceName":"1"}),"instanceName":"1"});
            var Q425;
            Q425=makeQuery(id+"F11.opPattern","COPY",BODY,{"derivedFrom":makeQuery(id+"F7.opPattern","COPY",BODY,{"derivedFrom":makeQuery(id+"F6.opPattern","COPY",BODY,{"derivedFrom":makeQuery(id+"F5.opPattern","COPY",BODY,{"derivedFrom":makeQuery(id+"F1.opRevolve","SWEPT_BODY",BODY,{"disambiguationData":[OSD([sQuery(id+"F0.wireOp",EDGE,"E1")])]}),"instanceName":"1"}),"instanceName":"1"}),"instanceName":"1"}),"instanceName":"1"});
            var Q426;
            Q426=makeQuery(id+"F11.opPattern","COPY",BODY,{"derivedFrom":makeQuery(id+"F7.opPattern","COPY",BODY,{"derivedFrom":makeQuery(id+"F6.opPattern","COPY",BODY,{"derivedFrom":makeQuery(id+"F5.opPattern","COPY",BODY,{"derivedFrom":makeQuery(id+"F2.opPattern","COPY",BODY,{"derivedFrom":makeQuery(id+"F1.opRevolve","SWEPT_BODY",BODY,{"disambiguationData":[OSD([sQuery(id+"F0.wireOp",EDGE,"E1")])]}),"instanceName":"1"}),"instanceName":"1"}),"instanceName":"1"}),"instanceName":"1"}),"instanceName":"1"});
            var Q427;
            Q427=makeQuery(id+"F11.opPattern","COPY",BODY,{"derivedFrom":makeQuery(id+"F7.opPattern","COPY",BODY,{"derivedFrom":makeQuery(id+"F6.opPattern","COPY",BODY,{"derivedFrom":makeQuery(id+"F5.opPattern","COPY",BODY,{"derivedFrom":makeQuery(id+"F3.opPattern","COPY",BODY,{"derivedFrom":makeQuery(id+"F2.opPattern","COPY",BODY,{"derivedFrom":makeQuery(id+"F1.opRevolve","SWEPT_BODY",BODY,{"disambiguationData":[OSD([sQuery(id+"F0.wireOp",EDGE,"E1")])]}),"instanceName":"1"}),"instanceName":"1"}),"instanceName":"1"}),"instanceName":"1"}),"instanceName":"1"}),"instanceName":"1"});
            var Q428;
            Q428=makeQuery(id+"F11.opPattern","COPY",BODY,{"derivedFrom":makeQuery(id+"F7.opPattern","COPY",BODY,{"derivedFrom":makeQuery(id+"F6.opPattern","COPY",BODY,{"derivedFrom":makeQuery(id+"F5.opPattern","COPY",BODY,{"derivedFrom":makeQuery(id+"F4.opPattern","COPY",BODY,{"derivedFrom":makeQuery(id+"F1.opRevolve","SWEPT_BODY",BODY,{"disambiguationData":[OSD([sQuery(id+"F0.wireOp",EDGE,"E1")])]}),"instanceName":"1"}),"instanceName":"1"}),"instanceName":"1"}),"instanceName":"1"}),"instanceName":"1"});
            var Q429;
            Q429=makeQuery(id+"F11.opPattern","COPY",BODY,{"derivedFrom":makeQuery(id+"F7.opPattern","COPY",BODY,{"derivedFrom":makeQuery(id+"F6.opPattern","COPY",BODY,{"derivedFrom":makeQuery(id+"F5.opPattern","COPY",BODY,{"derivedFrom":makeQuery(id+"F4.opPattern","COPY",BODY,{"derivedFrom":makeQuery(id+"F2.opPattern","COPY",BODY,{"derivedFrom":makeQuery(id+"F1.opRevolve","SWEPT_BODY",BODY,{"disambiguationData":[OSD([sQuery(id+"F0.wireOp",EDGE,"E1")])]}),"instanceName":"1"}),"instanceName":"1"}),"instanceName":"1"}),"instanceName":"1"}),"instanceName":"1"}),"instanceName":"1"});
            var Q430;
            Q430=makeQuery(id+"F11.opPattern","COPY",BODY,{"derivedFrom":makeQuery(id+"F7.opPattern","COPY",BODY,{"derivedFrom":makeQuery(id+"F6.opPattern","COPY",BODY,{"derivedFrom":makeQuery(id+"F5.opPattern","COPY",BODY,{"derivedFrom":makeQuery(id+"F4.opPattern","COPY",BODY,{"derivedFrom":makeQuery(id+"F3.opPattern","COPY",BODY,{"derivedFrom":makeQuery(id+"F2.opPattern","COPY",BODY,{"derivedFrom":makeQuery(id+"F1.opRevolve","SWEPT_BODY",BODY,{"disambiguationData":[OSD([sQuery(id+"F0.wireOp",EDGE,"E1")])]}),"instanceName":"1"}),"instanceName":"1"}),"instanceName":"1"}),"instanceName":"1"}),"instanceName":"1"}),"instanceName":"1"}),"instanceName":"1"});
            var Q431;
            Q431=makeQuery(id+"F11.opPattern","COPY",BODY,{"derivedFrom":makeQuery(id+"F8.opPattern","COPY",BODY,{"derivedFrom":makeQuery(id+"F1.opRevolve","SWEPT_BODY",BODY,{"disambiguationData":[OSD([sQuery(id+"F0.wireOp",EDGE,"E1")])]}),"instanceName":"1"}),"instanceName":"1"});
            var Q432;
            Q432=makeQuery(id+"F11.opPattern","COPY",BODY,{"derivedFrom":makeQuery(id+"F8.opPattern","COPY",BODY,{"derivedFrom":makeQuery(id+"F2.opPattern","COPY",BODY,{"derivedFrom":makeQuery(id+"F1.opRevolve","SWEPT_BODY",BODY,{"disambiguationData":[OSD([sQuery(id+"F0.wireOp",EDGE,"E1")])]}),"instanceName":"1"}),"instanceName":"1"}),"instanceName":"1"});
            var Q433;
            Q433=makeQuery(id+"F11.opPattern","COPY",BODY,{"derivedFrom":makeQuery(id+"F8.opPattern","COPY",BODY,{"derivedFrom":makeQuery(id+"F3.opPattern","COPY",BODY,{"derivedFrom":makeQuery(id+"F2.opPattern","COPY",BODY,{"derivedFrom":makeQuery(id+"F1.opRevolve","SWEPT_BODY",BODY,{"disambiguationData":[OSD([sQuery(id+"F0.wireOp",EDGE,"E1")])]}),"instanceName":"1"}),"instanceName":"1"}),"instanceName":"1"}),"instanceName":"1"});
            var Q434;
            Q434=makeQuery(id+"F11.opPattern","COPY",BODY,{"derivedFrom":makeQuery(id+"F8.opPattern","COPY",BODY,{"derivedFrom":makeQuery(id+"F4.opPattern","COPY",BODY,{"derivedFrom":makeQuery(id+"F1.opRevolve","SWEPT_BODY",BODY,{"disambiguationData":[OSD([sQuery(id+"F0.wireOp",EDGE,"E1")])]}),"instanceName":"1"}),"instanceName":"1"}),"instanceName":"1"});
            var Q435;
            Q435=makeQuery(id+"F11.opPattern","COPY",BODY,{"derivedFrom":makeQuery(id+"F8.opPattern","COPY",BODY,{"derivedFrom":makeQuery(id+"F4.opPattern","COPY",BODY,{"derivedFrom":makeQuery(id+"F2.opPattern","COPY",BODY,{"derivedFrom":makeQuery(id+"F1.opRevolve","SWEPT_BODY",BODY,{"disambiguationData":[OSD([sQuery(id+"F0.wireOp",EDGE,"E1")])]}),"instanceName":"1"}),"instanceName":"1"}),"instanceName":"1"}),"instanceName":"1"});
            var Q436;
            Q436=makeQuery(id+"F11.opPattern","COPY",BODY,{"derivedFrom":makeQuery(id+"F8.opPattern","COPY",BODY,{"derivedFrom":makeQuery(id+"F4.opPattern","COPY",BODY,{"derivedFrom":makeQuery(id+"F3.opPattern","COPY",BODY,{"derivedFrom":makeQuery(id+"F2.opPattern","COPY",BODY,{"derivedFrom":makeQuery(id+"F1.opRevolve","SWEPT_BODY",BODY,{"disambiguationData":[OSD([sQuery(id+"F0.wireOp",EDGE,"E1")])]}),"instanceName":"1"}),"instanceName":"1"}),"instanceName":"1"}),"instanceName":"1"}),"instanceName":"1"});
            var Q437;
            Q437=makeQuery(id+"F11.opPattern","COPY",BODY,{"derivedFrom":makeQuery(id+"F8.opPattern","COPY",BODY,{"derivedFrom":makeQuery(id+"F5.opPattern","COPY",BODY,{"derivedFrom":makeQuery(id+"F1.opRevolve","SWEPT_BODY",BODY,{"disambiguationData":[OSD([sQuery(id+"F0.wireOp",EDGE,"E1")])]}),"instanceName":"1"}),"instanceName":"1"}),"instanceName":"1"});
            var Q438;
            Q438=makeQuery(id+"F11.opPattern","COPY",BODY,{"derivedFrom":makeQuery(id+"F8.opPattern","COPY",BODY,{"derivedFrom":makeQuery(id+"F5.opPattern","COPY",BODY,{"derivedFrom":makeQuery(id+"F2.opPattern","COPY",BODY,{"derivedFrom":makeQuery(id+"F1.opRevolve","SWEPT_BODY",BODY,{"disambiguationData":[OSD([sQuery(id+"F0.wireOp",EDGE,"E1")])]}),"instanceName":"1"}),"instanceName":"1"}),"instanceName":"1"}),"instanceName":"1"});
            var Q439;
            Q439=makeQuery(id+"F11.opPattern","COPY",BODY,{"derivedFrom":makeQuery(id+"F8.opPattern","COPY",BODY,{"derivedFrom":makeQuery(id+"F5.opPattern","COPY",BODY,{"derivedFrom":makeQuery(id+"F3.opPattern","COPY",BODY,{"derivedFrom":makeQuery(id+"F2.opPattern","COPY",BODY,{"derivedFrom":makeQuery(id+"F1.opRevolve","SWEPT_BODY",BODY,{"disambiguationData":[OSD([sQuery(id+"F0.wireOp",EDGE,"E1")])]}),"instanceName":"1"}),"instanceName":"1"}),"instanceName":"1"}),"instanceName":"1"}),"instanceName":"1"});
            var Q440;
            Q440=makeQuery(id+"F11.opPattern","COPY",BODY,{"derivedFrom":makeQuery(id+"F8.opPattern","COPY",BODY,{"derivedFrom":makeQuery(id+"F5.opPattern","COPY",BODY,{"derivedFrom":makeQuery(id+"F4.opPattern","COPY",BODY,{"derivedFrom":makeQuery(id+"F1.opRevolve","SWEPT_BODY",BODY,{"disambiguationData":[OSD([sQuery(id+"F0.wireOp",EDGE,"E1")])]}),"instanceName":"1"}),"instanceName":"1"}),"instanceName":"1"}),"instanceName":"1"});
            var Q441;
            Q441=makeQuery(id+"F11.opPattern","COPY",BODY,{"derivedFrom":makeQuery(id+"F8.opPattern","COPY",BODY,{"derivedFrom":makeQuery(id+"F5.opPattern","COPY",BODY,{"derivedFrom":makeQuery(id+"F4.opPattern","COPY",BODY,{"derivedFrom":makeQuery(id+"F2.opPattern","COPY",BODY,{"derivedFrom":makeQuery(id+"F1.opRevolve","SWEPT_BODY",BODY,{"disambiguationData":[OSD([sQuery(id+"F0.wireOp",EDGE,"E1")])]}),"instanceName":"1"}),"instanceName":"1"}),"instanceName":"1"}),"instanceName":"1"}),"instanceName":"1"});
            var Q442;
            Q442=makeQuery(id+"F11.opPattern","COPY",BODY,{"derivedFrom":makeQuery(id+"F8.opPattern","COPY",BODY,{"derivedFrom":makeQuery(id+"F5.opPattern","COPY",BODY,{"derivedFrom":makeQuery(id+"F4.opPattern","COPY",BODY,{"derivedFrom":makeQuery(id+"F3.opPattern","COPY",BODY,{"derivedFrom":makeQuery(id+"F2.opPattern","COPY",BODY,{"derivedFrom":makeQuery(id+"F1.opRevolve","SWEPT_BODY",BODY,{"disambiguationData":[OSD([sQuery(id+"F0.wireOp",EDGE,"E1")])]}),"instanceName":"1"}),"instanceName":"1"}),"instanceName":"1"}),"instanceName":"1"}),"instanceName":"1"}),"instanceName":"1"});
            var Q443;
            Q443=makeQuery(id+"F11.opPattern","COPY",BODY,{"derivedFrom":makeQuery(id+"F8.opPattern","COPY",BODY,{"derivedFrom":makeQuery(id+"F6.opPattern","COPY",BODY,{"derivedFrom":makeQuery(id+"F1.opRevolve","SWEPT_BODY",BODY,{"disambiguationData":[OSD([sQuery(id+"F0.wireOp",EDGE,"E1")])]}),"instanceName":"1"}),"instanceName":"1"}),"instanceName":"1"});
            var Q444;
            Q444=makeQuery(id+"F11.opPattern","COPY",BODY,{"derivedFrom":makeQuery(id+"F8.opPattern","COPY",BODY,{"derivedFrom":makeQuery(id+"F6.opPattern","COPY",BODY,{"derivedFrom":makeQuery(id+"F2.opPattern","COPY",BODY,{"derivedFrom":makeQuery(id+"F1.opRevolve","SWEPT_BODY",BODY,{"disambiguationData":[OSD([sQuery(id+"F0.wireOp",EDGE,"E1")])]}),"instanceName":"1"}),"instanceName":"1"}),"instanceName":"1"}),"instanceName":"1"});
            var Q445;
            Q445=makeQuery(id+"F11.opPattern","COPY",BODY,{"derivedFrom":makeQuery(id+"F8.opPattern","COPY",BODY,{"derivedFrom":makeQuery(id+"F6.opPattern","COPY",BODY,{"derivedFrom":makeQuery(id+"F3.opPattern","COPY",BODY,{"derivedFrom":makeQuery(id+"F2.opPattern","COPY",BODY,{"derivedFrom":makeQuery(id+"F1.opRevolve","SWEPT_BODY",BODY,{"disambiguationData":[OSD([sQuery(id+"F0.wireOp",EDGE,"E1")])]}),"instanceName":"1"}),"instanceName":"1"}),"instanceName":"1"}),"instanceName":"1"}),"instanceName":"1"});
            var Q446;
            Q446=makeQuery(id+"F11.opPattern","COPY",BODY,{"derivedFrom":makeQuery(id+"F8.opPattern","COPY",BODY,{"derivedFrom":makeQuery(id+"F6.opPattern","COPY",BODY,{"derivedFrom":makeQuery(id+"F4.opPattern","COPY",BODY,{"derivedFrom":makeQuery(id+"F1.opRevolve","SWEPT_BODY",BODY,{"disambiguationData":[OSD([sQuery(id+"F0.wireOp",EDGE,"E1")])]}),"instanceName":"1"}),"instanceName":"1"}),"instanceName":"1"}),"instanceName":"1"});
            var Q447;
            Q447=makeQuery(id+"F11.opPattern","COPY",BODY,{"derivedFrom":makeQuery(id+"F8.opPattern","COPY",BODY,{"derivedFrom":makeQuery(id+"F6.opPattern","COPY",BODY,{"derivedFrom":makeQuery(id+"F4.opPattern","COPY",BODY,{"derivedFrom":makeQuery(id+"F2.opPattern","COPY",BODY,{"derivedFrom":makeQuery(id+"F1.opRevolve","SWEPT_BODY",BODY,{"disambiguationData":[OSD([sQuery(id+"F0.wireOp",EDGE,"E1")])]}),"instanceName":"1"}),"instanceName":"1"}),"instanceName":"1"}),"instanceName":"1"}),"instanceName":"1"});
            var Q448;
            Q448=makeQuery(id+"F11.opPattern","COPY",BODY,{"derivedFrom":makeQuery(id+"F8.opPattern","COPY",BODY,{"derivedFrom":makeQuery(id+"F6.opPattern","COPY",BODY,{"derivedFrom":makeQuery(id+"F4.opPattern","COPY",BODY,{"derivedFrom":makeQuery(id+"F3.opPattern","COPY",BODY,{"derivedFrom":makeQuery(id+"F2.opPattern","COPY",BODY,{"derivedFrom":makeQuery(id+"F1.opRevolve","SWEPT_BODY",BODY,{"disambiguationData":[OSD([sQuery(id+"F0.wireOp",EDGE,"E1")])]}),"instanceName":"1"}),"instanceName":"1"}),"instanceName":"1"}),"instanceName":"1"}),"instanceName":"1"}),"instanceName":"1"});
            var Q449;
            Q449=makeQuery(id+"F11.opPattern","COPY",BODY,{"derivedFrom":makeQuery(id+"F8.opPattern","COPY",BODY,{"derivedFrom":makeQuery(id+"F6.opPattern","COPY",BODY,{"derivedFrom":makeQuery(id+"F5.opPattern","COPY",BODY,{"derivedFrom":makeQuery(id+"F1.opRevolve","SWEPT_BODY",BODY,{"disambiguationData":[OSD([sQuery(id+"F0.wireOp",EDGE,"E1")])]}),"instanceName":"1"}),"instanceName":"1"}),"instanceName":"1"}),"instanceName":"1"});
            var Q450;
            Q450=makeQuery(id+"F11.opPattern","COPY",BODY,{"derivedFrom":makeQuery(id+"F8.opPattern","COPY",BODY,{"derivedFrom":makeQuery(id+"F6.opPattern","COPY",BODY,{"derivedFrom":makeQuery(id+"F5.opPattern","COPY",BODY,{"derivedFrom":makeQuery(id+"F2.opPattern","COPY",BODY,{"derivedFrom":makeQuery(id+"F1.opRevolve","SWEPT_BODY",BODY,{"disambiguationData":[OSD([sQuery(id+"F0.wireOp",EDGE,"E1")])]}),"instanceName":"1"}),"instanceName":"1"}),"instanceName":"1"}),"instanceName":"1"}),"instanceName":"1"});
            var Q451;
            Q451=makeQuery(id+"F11.opPattern","COPY",BODY,{"derivedFrom":makeQuery(id+"F8.opPattern","COPY",BODY,{"derivedFrom":makeQuery(id+"F6.opPattern","COPY",BODY,{"derivedFrom":makeQuery(id+"F5.opPattern","COPY",BODY,{"derivedFrom":makeQuery(id+"F3.opPattern","COPY",BODY,{"derivedFrom":makeQuery(id+"F2.opPattern","COPY",BODY,{"derivedFrom":makeQuery(id+"F1.opRevolve","SWEPT_BODY",BODY,{"disambiguationData":[OSD([sQuery(id+"F0.wireOp",EDGE,"E1")])]}),"instanceName":"1"}),"instanceName":"1"}),"instanceName":"1"}),"instanceName":"1"}),"instanceName":"1"}),"instanceName":"1"});
            var Q452;
            Q452=makeQuery(id+"F11.opPattern","COPY",BODY,{"derivedFrom":makeQuery(id+"F8.opPattern","COPY",BODY,{"derivedFrom":makeQuery(id+"F6.opPattern","COPY",BODY,{"derivedFrom":makeQuery(id+"F5.opPattern","COPY",BODY,{"derivedFrom":makeQuery(id+"F4.opPattern","COPY",BODY,{"derivedFrom":makeQuery(id+"F1.opRevolve","SWEPT_BODY",BODY,{"disambiguationData":[OSD([sQuery(id+"F0.wireOp",EDGE,"E1")])]}),"instanceName":"1"}),"instanceName":"1"}),"instanceName":"1"}),"instanceName":"1"}),"instanceName":"1"});
            var Q453;
            Q453=makeQuery(id+"F11.opPattern","COPY",BODY,{"derivedFrom":makeQuery(id+"F8.opPattern","COPY",BODY,{"derivedFrom":makeQuery(id+"F6.opPattern","COPY",BODY,{"derivedFrom":makeQuery(id+"F5.opPattern","COPY",BODY,{"derivedFrom":makeQuery(id+"F4.opPattern","COPY",BODY,{"derivedFrom":makeQuery(id+"F2.opPattern","COPY",BODY,{"derivedFrom":makeQuery(id+"F1.opRevolve","SWEPT_BODY",BODY,{"disambiguationData":[OSD([sQuery(id+"F0.wireOp",EDGE,"E1")])]}),"instanceName":"1"}),"instanceName":"1"}),"instanceName":"1"}),"instanceName":"1"}),"instanceName":"1"}),"instanceName":"1"});
            var Q454;
            Q454=makeQuery(id+"F11.opPattern","COPY",BODY,{"derivedFrom":makeQuery(id+"F8.opPattern","COPY",BODY,{"derivedFrom":makeQuery(id+"F6.opPattern","COPY",BODY,{"derivedFrom":makeQuery(id+"F5.opPattern","COPY",BODY,{"derivedFrom":makeQuery(id+"F4.opPattern","COPY",BODY,{"derivedFrom":makeQuery(id+"F3.opPattern","COPY",BODY,{"derivedFrom":makeQuery(id+"F2.opPattern","COPY",BODY,{"derivedFrom":makeQuery(id+"F1.opRevolve","SWEPT_BODY",BODY,{"disambiguationData":[OSD([sQuery(id+"F0.wireOp",EDGE,"E1")])]}),"instanceName":"1"}),"instanceName":"1"}),"instanceName":"1"}),"instanceName":"1"}),"instanceName":"1"}),"instanceName":"1"}),"instanceName":"1"});
            var Q455;
            Q455=makeQuery(id+"F11.opPattern","COPY",BODY,{"derivedFrom":makeQuery(id+"F8.opPattern","COPY",BODY,{"derivedFrom":makeQuery(id+"F7.opPattern","COPY",BODY,{"derivedFrom":makeQuery(id+"F1.opRevolve","SWEPT_BODY",BODY,{"disambiguationData":[OSD([sQuery(id+"F0.wireOp",EDGE,"E1")])]}),"instanceName":"1"}),"instanceName":"1"}),"instanceName":"1"});
            var Q456;
            Q456=makeQuery(id+"F11.opPattern","COPY",BODY,{"derivedFrom":makeQuery(id+"F8.opPattern","COPY",BODY,{"derivedFrom":makeQuery(id+"F7.opPattern","COPY",BODY,{"derivedFrom":makeQuery(id+"F2.opPattern","COPY",BODY,{"derivedFrom":makeQuery(id+"F1.opRevolve","SWEPT_BODY",BODY,{"disambiguationData":[OSD([sQuery(id+"F0.wireOp",EDGE,"E1")])]}),"instanceName":"1"}),"instanceName":"1"}),"instanceName":"1"}),"instanceName":"1"});
            var Q457;
            Q457=makeQuery(id+"F11.opPattern","COPY",BODY,{"derivedFrom":makeQuery(id+"F8.opPattern","COPY",BODY,{"derivedFrom":makeQuery(id+"F7.opPattern","COPY",BODY,{"derivedFrom":makeQuery(id+"F3.opPattern","COPY",BODY,{"derivedFrom":makeQuery(id+"F2.opPattern","COPY",BODY,{"derivedFrom":makeQuery(id+"F1.opRevolve","SWEPT_BODY",BODY,{"disambiguationData":[OSD([sQuery(id+"F0.wireOp",EDGE,"E1")])]}),"instanceName":"1"}),"instanceName":"1"}),"instanceName":"1"}),"instanceName":"1"}),"instanceName":"1"});
            var Q458;
            Q458=makeQuery(id+"F11.opPattern","COPY",BODY,{"derivedFrom":makeQuery(id+"F8.opPattern","COPY",BODY,{"derivedFrom":makeQuery(id+"F7.opPattern","COPY",BODY,{"derivedFrom":makeQuery(id+"F4.opPattern","COPY",BODY,{"derivedFrom":makeQuery(id+"F1.opRevolve","SWEPT_BODY",BODY,{"disambiguationData":[OSD([sQuery(id+"F0.wireOp",EDGE,"E1")])]}),"instanceName":"1"}),"instanceName":"1"}),"instanceName":"1"}),"instanceName":"1"});
            var Q459;
            Q459=makeQuery(id+"F11.opPattern","COPY",BODY,{"derivedFrom":makeQuery(id+"F8.opPattern","COPY",BODY,{"derivedFrom":makeQuery(id+"F7.opPattern","COPY",BODY,{"derivedFrom":makeQuery(id+"F4.opPattern","COPY",BODY,{"derivedFrom":makeQuery(id+"F2.opPattern","COPY",BODY,{"derivedFrom":makeQuery(id+"F1.opRevolve","SWEPT_BODY",BODY,{"disambiguationData":[OSD([sQuery(id+"F0.wireOp",EDGE,"E1")])]}),"instanceName":"1"}),"instanceName":"1"}),"instanceName":"1"}),"instanceName":"1"}),"instanceName":"1"});
            var Q460;
            Q460=makeQuery(id+"F11.opPattern","COPY",BODY,{"derivedFrom":makeQuery(id+"F8.opPattern","COPY",BODY,{"derivedFrom":makeQuery(id+"F7.opPattern","COPY",BODY,{"derivedFrom":makeQuery(id+"F4.opPattern","COPY",BODY,{"derivedFrom":makeQuery(id+"F3.opPattern","COPY",BODY,{"derivedFrom":makeQuery(id+"F2.opPattern","COPY",BODY,{"derivedFrom":makeQuery(id+"F1.opRevolve","SWEPT_BODY",BODY,{"disambiguationData":[OSD([sQuery(id+"F0.wireOp",EDGE,"E1")])]}),"instanceName":"1"}),"instanceName":"1"}),"instanceName":"1"}),"instanceName":"1"}),"instanceName":"1"}),"instanceName":"1"});
            var Q461;
            Q461=makeQuery(id+"F11.opPattern","COPY",BODY,{"derivedFrom":makeQuery(id+"F8.opPattern","COPY",BODY,{"derivedFrom":makeQuery(id+"F7.opPattern","COPY",BODY,{"derivedFrom":makeQuery(id+"F5.opPattern","COPY",BODY,{"derivedFrom":makeQuery(id+"F1.opRevolve","SWEPT_BODY",BODY,{"disambiguationData":[OSD([sQuery(id+"F0.wireOp",EDGE,"E1")])]}),"instanceName":"1"}),"instanceName":"1"}),"instanceName":"1"}),"instanceName":"1"});
            var Q462;
            Q462=makeQuery(id+"F11.opPattern","COPY",BODY,{"derivedFrom":makeQuery(id+"F8.opPattern","COPY",BODY,{"derivedFrom":makeQuery(id+"F7.opPattern","COPY",BODY,{"derivedFrom":makeQuery(id+"F5.opPattern","COPY",BODY,{"derivedFrom":makeQuery(id+"F2.opPattern","COPY",BODY,{"derivedFrom":makeQuery(id+"F1.opRevolve","SWEPT_BODY",BODY,{"disambiguationData":[OSD([sQuery(id+"F0.wireOp",EDGE,"E1")])]}),"instanceName":"1"}),"instanceName":"1"}),"instanceName":"1"}),"instanceName":"1"}),"instanceName":"1"});
            var Q463;
            Q463=makeQuery(id+"F11.opPattern","COPY",BODY,{"derivedFrom":makeQuery(id+"F8.opPattern","COPY",BODY,{"derivedFrom":makeQuery(id+"F7.opPattern","COPY",BODY,{"derivedFrom":makeQuery(id+"F5.opPattern","COPY",BODY,{"derivedFrom":makeQuery(id+"F3.opPattern","COPY",BODY,{"derivedFrom":makeQuery(id+"F2.opPattern","COPY",BODY,{"derivedFrom":makeQuery(id+"F1.opRevolve","SWEPT_BODY",BODY,{"disambiguationData":[OSD([sQuery(id+"F0.wireOp",EDGE,"E1")])]}),"instanceName":"1"}),"instanceName":"1"}),"instanceName":"1"}),"instanceName":"1"}),"instanceName":"1"}),"instanceName":"1"});
            var Q464;
            Q464=makeQuery(id+"F11.opPattern","COPY",BODY,{"derivedFrom":makeQuery(id+"F8.opPattern","COPY",BODY,{"derivedFrom":makeQuery(id+"F7.opPattern","COPY",BODY,{"derivedFrom":makeQuery(id+"F5.opPattern","COPY",BODY,{"derivedFrom":makeQuery(id+"F4.opPattern","COPY",BODY,{"derivedFrom":makeQuery(id+"F1.opRevolve","SWEPT_BODY",BODY,{"disambiguationData":[OSD([sQuery(id+"F0.wireOp",EDGE,"E1")])]}),"instanceName":"1"}),"instanceName":"1"}),"instanceName":"1"}),"instanceName":"1"}),"instanceName":"1"});
            var Q465;
            Q465=makeQuery(id+"F11.opPattern","COPY",BODY,{"derivedFrom":makeQuery(id+"F8.opPattern","COPY",BODY,{"derivedFrom":makeQuery(id+"F7.opPattern","COPY",BODY,{"derivedFrom":makeQuery(id+"F5.opPattern","COPY",BODY,{"derivedFrom":makeQuery(id+"F4.opPattern","COPY",BODY,{"derivedFrom":makeQuery(id+"F2.opPattern","COPY",BODY,{"derivedFrom":makeQuery(id+"F1.opRevolve","SWEPT_BODY",BODY,{"disambiguationData":[OSD([sQuery(id+"F0.wireOp",EDGE,"E1")])]}),"instanceName":"1"}),"instanceName":"1"}),"instanceName":"1"}),"instanceName":"1"}),"instanceName":"1"}),"instanceName":"1"});
            var Q466;
            Q466=makeQuery(id+"F11.opPattern","COPY",BODY,{"derivedFrom":makeQuery(id+"F8.opPattern","COPY",BODY,{"derivedFrom":makeQuery(id+"F7.opPattern","COPY",BODY,{"derivedFrom":makeQuery(id+"F5.opPattern","COPY",BODY,{"derivedFrom":makeQuery(id+"F4.opPattern","COPY",BODY,{"derivedFrom":makeQuery(id+"F3.opPattern","COPY",BODY,{"derivedFrom":makeQuery(id+"F2.opPattern","COPY",BODY,{"derivedFrom":makeQuery(id+"F1.opRevolve","SWEPT_BODY",BODY,{"disambiguationData":[OSD([sQuery(id+"F0.wireOp",EDGE,"E1")])]}),"instanceName":"1"}),"instanceName":"1"}),"instanceName":"1"}),"instanceName":"1"}),"instanceName":"1"}),"instanceName":"1"}),"instanceName":"1"});
            var Q467;
            Q467=makeQuery(id+"F11.opPattern","COPY",BODY,{"derivedFrom":makeQuery(id+"F8.opPattern","COPY",BODY,{"derivedFrom":makeQuery(id+"F7.opPattern","COPY",BODY,{"derivedFrom":makeQuery(id+"F6.opPattern","COPY",BODY,{"derivedFrom":makeQuery(id+"F1.opRevolve","SWEPT_BODY",BODY,{"disambiguationData":[OSD([sQuery(id+"F0.wireOp",EDGE,"E1")])]}),"instanceName":"1"}),"instanceName":"1"}),"instanceName":"1"}),"instanceName":"1"});
            var Q468;
            Q468=makeQuery(id+"F11.opPattern","COPY",BODY,{"derivedFrom":makeQuery(id+"F8.opPattern","COPY",BODY,{"derivedFrom":makeQuery(id+"F7.opPattern","COPY",BODY,{"derivedFrom":makeQuery(id+"F6.opPattern","COPY",BODY,{"derivedFrom":makeQuery(id+"F2.opPattern","COPY",BODY,{"derivedFrom":makeQuery(id+"F1.opRevolve","SWEPT_BODY",BODY,{"disambiguationData":[OSD([sQuery(id+"F0.wireOp",EDGE,"E1")])]}),"instanceName":"1"}),"instanceName":"1"}),"instanceName":"1"}),"instanceName":"1"}),"instanceName":"1"});
            var Q469;
            Q469=makeQuery(id+"F11.opPattern","COPY",BODY,{"derivedFrom":makeQuery(id+"F8.opPattern","COPY",BODY,{"derivedFrom":makeQuery(id+"F7.opPattern","COPY",BODY,{"derivedFrom":makeQuery(id+"F6.opPattern","COPY",BODY,{"derivedFrom":makeQuery(id+"F3.opPattern","COPY",BODY,{"derivedFrom":makeQuery(id+"F2.opPattern","COPY",BODY,{"derivedFrom":makeQuery(id+"F1.opRevolve","SWEPT_BODY",BODY,{"disambiguationData":[OSD([sQuery(id+"F0.wireOp",EDGE,"E1")])]}),"instanceName":"1"}),"instanceName":"1"}),"instanceName":"1"}),"instanceName":"1"}),"instanceName":"1"}),"instanceName":"1"});
            var Q470;
            Q470=makeQuery(id+"F11.opPattern","COPY",BODY,{"derivedFrom":makeQuery(id+"F8.opPattern","COPY",BODY,{"derivedFrom":makeQuery(id+"F7.opPattern","COPY",BODY,{"derivedFrom":makeQuery(id+"F6.opPattern","COPY",BODY,{"derivedFrom":makeQuery(id+"F4.opPattern","COPY",BODY,{"derivedFrom":makeQuery(id+"F1.opRevolve","SWEPT_BODY",BODY,{"disambiguationData":[OSD([sQuery(id+"F0.wireOp",EDGE,"E1")])]}),"instanceName":"1"}),"instanceName":"1"}),"instanceName":"1"}),"instanceName":"1"}),"instanceName":"1"});
            var Q471;
            Q471=makeQuery(id+"F11.opPattern","COPY",BODY,{"derivedFrom":makeQuery(id+"F8.opPattern","COPY",BODY,{"derivedFrom":makeQuery(id+"F7.opPattern","COPY",BODY,{"derivedFrom":makeQuery(id+"F6.opPattern","COPY",BODY,{"derivedFrom":makeQuery(id+"F4.opPattern","COPY",BODY,{"derivedFrom":makeQuery(id+"F2.opPattern","COPY",BODY,{"derivedFrom":makeQuery(id+"F1.opRevolve","SWEPT_BODY",BODY,{"disambiguationData":[OSD([sQuery(id+"F0.wireOp",EDGE,"E1")])]}),"instanceName":"1"}),"instanceName":"1"}),"instanceName":"1"}),"instanceName":"1"}),"instanceName":"1"}),"instanceName":"1"});
            var Q472;
            Q472=makeQuery(id+"F11.opPattern","COPY",BODY,{"derivedFrom":makeQuery(id+"F8.opPattern","COPY",BODY,{"derivedFrom":makeQuery(id+"F7.opPattern","COPY",BODY,{"derivedFrom":makeQuery(id+"F6.opPattern","COPY",BODY,{"derivedFrom":makeQuery(id+"F4.opPattern","COPY",BODY,{"derivedFrom":makeQuery(id+"F3.opPattern","COPY",BODY,{"derivedFrom":makeQuery(id+"F2.opPattern","COPY",BODY,{"derivedFrom":makeQuery(id+"F1.opRevolve","SWEPT_BODY",BODY,{"disambiguationData":[OSD([sQuery(id+"F0.wireOp",EDGE,"E1")])]}),"instanceName":"1"}),"instanceName":"1"}),"instanceName":"1"}),"instanceName":"1"}),"instanceName":"1"}),"instanceName":"1"}),"instanceName":"1"});
            var Q473;
            Q473=makeQuery(id+"F11.opPattern","COPY",BODY,{"derivedFrom":makeQuery(id+"F8.opPattern","COPY",BODY,{"derivedFrom":makeQuery(id+"F7.opPattern","COPY",BODY,{"derivedFrom":makeQuery(id+"F6.opPattern","COPY",BODY,{"derivedFrom":makeQuery(id+"F5.opPattern","COPY",BODY,{"derivedFrom":makeQuery(id+"F1.opRevolve","SWEPT_BODY",BODY,{"disambiguationData":[OSD([sQuery(id+"F0.wireOp",EDGE,"E1")])]}),"instanceName":"1"}),"instanceName":"1"}),"instanceName":"1"}),"instanceName":"1"}),"instanceName":"1"});
            var Q474;
            Q474=makeQuery(id+"F11.opPattern","COPY",BODY,{"derivedFrom":makeQuery(id+"F8.opPattern","COPY",BODY,{"derivedFrom":makeQuery(id+"F7.opPattern","COPY",BODY,{"derivedFrom":makeQuery(id+"F6.opPattern","COPY",BODY,{"derivedFrom":makeQuery(id+"F5.opPattern","COPY",BODY,{"derivedFrom":makeQuery(id+"F2.opPattern","COPY",BODY,{"derivedFrom":makeQuery(id+"F1.opRevolve","SWEPT_BODY",BODY,{"disambiguationData":[OSD([sQuery(id+"F0.wireOp",EDGE,"E1")])]}),"instanceName":"1"}),"instanceName":"1"}),"instanceName":"1"}),"instanceName":"1"}),"instanceName":"1"}),"instanceName":"1"});
            var Q475;
            Q475=makeQuery(id+"F11.opPattern","COPY",BODY,{"derivedFrom":makeQuery(id+"F8.opPattern","COPY",BODY,{"derivedFrom":makeQuery(id+"F7.opPattern","COPY",BODY,{"derivedFrom":makeQuery(id+"F6.opPattern","COPY",BODY,{"derivedFrom":makeQuery(id+"F5.opPattern","COPY",BODY,{"derivedFrom":makeQuery(id+"F3.opPattern","COPY",BODY,{"derivedFrom":makeQuery(id+"F2.opPattern","COPY",BODY,{"derivedFrom":makeQuery(id+"F1.opRevolve","SWEPT_BODY",BODY,{"disambiguationData":[OSD([sQuery(id+"F0.wireOp",EDGE,"E1")])]}),"instanceName":"1"}),"instanceName":"1"}),"instanceName":"1"}),"instanceName":"1"}),"instanceName":"1"}),"instanceName":"1"}),"instanceName":"1"});
            var Q476;
            Q476=makeQuery(id+"F11.opPattern","COPY",BODY,{"derivedFrom":makeQuery(id+"F8.opPattern","COPY",BODY,{"derivedFrom":makeQuery(id+"F7.opPattern","COPY",BODY,{"derivedFrom":makeQuery(id+"F6.opPattern","COPY",BODY,{"derivedFrom":makeQuery(id+"F5.opPattern","COPY",BODY,{"derivedFrom":makeQuery(id+"F4.opPattern","COPY",BODY,{"derivedFrom":makeQuery(id+"F1.opRevolve","SWEPT_BODY",BODY,{"disambiguationData":[OSD([sQuery(id+"F0.wireOp",EDGE,"E1")])]}),"instanceName":"1"}),"instanceName":"1"}),"instanceName":"1"}),"instanceName":"1"}),"instanceName":"1"}),"instanceName":"1"});
            var Q477;
            Q477=makeQuery(id+"F11.opPattern","COPY",BODY,{"derivedFrom":makeQuery(id+"F8.opPattern","COPY",BODY,{"derivedFrom":makeQuery(id+"F7.opPattern","COPY",BODY,{"derivedFrom":makeQuery(id+"F6.opPattern","COPY",BODY,{"derivedFrom":makeQuery(id+"F5.opPattern","COPY",BODY,{"derivedFrom":makeQuery(id+"F4.opPattern","COPY",BODY,{"derivedFrom":makeQuery(id+"F2.opPattern","COPY",BODY,{"derivedFrom":makeQuery(id+"F1.opRevolve","SWEPT_BODY",BODY,{"disambiguationData":[OSD([sQuery(id+"F0.wireOp",EDGE,"E1")])]}),"instanceName":"1"}),"instanceName":"1"}),"instanceName":"1"}),"instanceName":"1"}),"instanceName":"1"}),"instanceName":"1"}),"instanceName":"1"});
            var Q478;
            Q478=makeQuery(id+"F11.opPattern","COPY",BODY,{"derivedFrom":makeQuery(id+"F8.opPattern","COPY",BODY,{"derivedFrom":makeQuery(id+"F7.opPattern","COPY",BODY,{"derivedFrom":makeQuery(id+"F6.opPattern","COPY",BODY,{"derivedFrom":makeQuery(id+"F5.opPattern","COPY",BODY,{"derivedFrom":makeQuery(id+"F4.opPattern","COPY",BODY,{"derivedFrom":makeQuery(id+"F3.opPattern","COPY",BODY,{"derivedFrom":makeQuery(id+"F2.opPattern","COPY",BODY,{"derivedFrom":makeQuery(id+"F1.opRevolve","SWEPT_BODY",BODY,{"disambiguationData":[OSD([sQuery(id+"F0.wireOp",EDGE,"E1")])]}),"instanceName":"1"}),"instanceName":"1"}),"instanceName":"1"}),"instanceName":"1"}),"instanceName":"1"}),"instanceName":"1"}),"instanceName":"1"}),"instanceName":"1"});
            var Q479;
            Q479=makeQuery(id+"F11.opPattern","COPY",BODY,{"derivedFrom":makeQuery(id+"F9.opPattern","COPY",BODY,{"derivedFrom":makeQuery(id+"F1.opRevolve","SWEPT_BODY",BODY,{"disambiguationData":[OSD([sQuery(id+"F0.wireOp",EDGE,"E1")])]}),"instanceName":"1"}),"instanceName":"1"});
            var Q480;
            Q480=makeQuery(id+"F11.opPattern","COPY",BODY,{"derivedFrom":makeQuery(id+"F9.opPattern","COPY",BODY,{"derivedFrom":makeQuery(id+"F2.opPattern","COPY",BODY,{"derivedFrom":makeQuery(id+"F1.opRevolve","SWEPT_BODY",BODY,{"disambiguationData":[OSD([sQuery(id+"F0.wireOp",EDGE,"E1")])]}),"instanceName":"1"}),"instanceName":"1"}),"instanceName":"1"});
            var Q481;
            Q481=makeQuery(id+"F11.opPattern","COPY",BODY,{"derivedFrom":makeQuery(id+"F9.opPattern","COPY",BODY,{"derivedFrom":makeQuery(id+"F3.opPattern","COPY",BODY,{"derivedFrom":makeQuery(id+"F2.opPattern","COPY",BODY,{"derivedFrom":makeQuery(id+"F1.opRevolve","SWEPT_BODY",BODY,{"disambiguationData":[OSD([sQuery(id+"F0.wireOp",EDGE,"E1")])]}),"instanceName":"1"}),"instanceName":"1"}),"instanceName":"1"}),"instanceName":"1"});
            var Q482;
            Q482=makeQuery(id+"F11.opPattern","COPY",BODY,{"derivedFrom":makeQuery(id+"F9.opPattern","COPY",BODY,{"derivedFrom":makeQuery(id+"F4.opPattern","COPY",BODY,{"derivedFrom":makeQuery(id+"F1.opRevolve","SWEPT_BODY",BODY,{"disambiguationData":[OSD([sQuery(id+"F0.wireOp",EDGE,"E1")])]}),"instanceName":"1"}),"instanceName":"1"}),"instanceName":"1"});
            var Q483;
            Q483=makeQuery(id+"F11.opPattern","COPY",BODY,{"derivedFrom":makeQuery(id+"F9.opPattern","COPY",BODY,{"derivedFrom":makeQuery(id+"F4.opPattern","COPY",BODY,{"derivedFrom":makeQuery(id+"F2.opPattern","COPY",BODY,{"derivedFrom":makeQuery(id+"F1.opRevolve","SWEPT_BODY",BODY,{"disambiguationData":[OSD([sQuery(id+"F0.wireOp",EDGE,"E1")])]}),"instanceName":"1"}),"instanceName":"1"}),"instanceName":"1"}),"instanceName":"1"});
            var Q484;
            Q484=makeQuery(id+"F11.opPattern","COPY",BODY,{"derivedFrom":makeQuery(id+"F9.opPattern","COPY",BODY,{"derivedFrom":makeQuery(id+"F4.opPattern","COPY",BODY,{"derivedFrom":makeQuery(id+"F3.opPattern","COPY",BODY,{"derivedFrom":makeQuery(id+"F2.opPattern","COPY",BODY,{"derivedFrom":makeQuery(id+"F1.opRevolve","SWEPT_BODY",BODY,{"disambiguationData":[OSD([sQuery(id+"F0.wireOp",EDGE,"E1")])]}),"instanceName":"1"}),"instanceName":"1"}),"instanceName":"1"}),"instanceName":"1"}),"instanceName":"1"});
            var Q485;
            Q485=makeQuery(id+"F11.opPattern","COPY",BODY,{"derivedFrom":makeQuery(id+"F9.opPattern","COPY",BODY,{"derivedFrom":makeQuery(id+"F5.opPattern","COPY",BODY,{"derivedFrom":makeQuery(id+"F1.opRevolve","SWEPT_BODY",BODY,{"disambiguationData":[OSD([sQuery(id+"F0.wireOp",EDGE,"E1")])]}),"instanceName":"1"}),"instanceName":"1"}),"instanceName":"1"});
            var Q486;
            Q486=makeQuery(id+"F11.opPattern","COPY",BODY,{"derivedFrom":makeQuery(id+"F9.opPattern","COPY",BODY,{"derivedFrom":makeQuery(id+"F5.opPattern","COPY",BODY,{"derivedFrom":makeQuery(id+"F2.opPattern","COPY",BODY,{"derivedFrom":makeQuery(id+"F1.opRevolve","SWEPT_BODY",BODY,{"disambiguationData":[OSD([sQuery(id+"F0.wireOp",EDGE,"E1")])]}),"instanceName":"1"}),"instanceName":"1"}),"instanceName":"1"}),"instanceName":"1"});
            var Q487;
            Q487=makeQuery(id+"F11.opPattern","COPY",BODY,{"derivedFrom":makeQuery(id+"F9.opPattern","COPY",BODY,{"derivedFrom":makeQuery(id+"F5.opPattern","COPY",BODY,{"derivedFrom":makeQuery(id+"F3.opPattern","COPY",BODY,{"derivedFrom":makeQuery(id+"F2.opPattern","COPY",BODY,{"derivedFrom":makeQuery(id+"F1.opRevolve","SWEPT_BODY",BODY,{"disambiguationData":[OSD([sQuery(id+"F0.wireOp",EDGE,"E1")])]}),"instanceName":"1"}),"instanceName":"1"}),"instanceName":"1"}),"instanceName":"1"}),"instanceName":"1"});
            var Q488;
            Q488=makeQuery(id+"F11.opPattern","COPY",BODY,{"derivedFrom":makeQuery(id+"F9.opPattern","COPY",BODY,{"derivedFrom":makeQuery(id+"F5.opPattern","COPY",BODY,{"derivedFrom":makeQuery(id+"F4.opPattern","COPY",BODY,{"derivedFrom":makeQuery(id+"F1.opRevolve","SWEPT_BODY",BODY,{"disambiguationData":[OSD([sQuery(id+"F0.wireOp",EDGE,"E1")])]}),"instanceName":"1"}),"instanceName":"1"}),"instanceName":"1"}),"instanceName":"1"});
            var Q489;
            Q489=makeQuery(id+"F11.opPattern","COPY",BODY,{"derivedFrom":makeQuery(id+"F9.opPattern","COPY",BODY,{"derivedFrom":makeQuery(id+"F5.opPattern","COPY",BODY,{"derivedFrom":makeQuery(id+"F4.opPattern","COPY",BODY,{"derivedFrom":makeQuery(id+"F2.opPattern","COPY",BODY,{"derivedFrom":makeQuery(id+"F1.opRevolve","SWEPT_BODY",BODY,{"disambiguationData":[OSD([sQuery(id+"F0.wireOp",EDGE,"E1")])]}),"instanceName":"1"}),"instanceName":"1"}),"instanceName":"1"}),"instanceName":"1"}),"instanceName":"1"});
            var Q490;
            Q490=makeQuery(id+"F11.opPattern","COPY",BODY,{"derivedFrom":makeQuery(id+"F9.opPattern","COPY",BODY,{"derivedFrom":makeQuery(id+"F5.opPattern","COPY",BODY,{"derivedFrom":makeQuery(id+"F4.opPattern","COPY",BODY,{"derivedFrom":makeQuery(id+"F3.opPattern","COPY",BODY,{"derivedFrom":makeQuery(id+"F2.opPattern","COPY",BODY,{"derivedFrom":makeQuery(id+"F1.opRevolve","SWEPT_BODY",BODY,{"disambiguationData":[OSD([sQuery(id+"F0.wireOp",EDGE,"E1")])]}),"instanceName":"1"}),"instanceName":"1"}),"instanceName":"1"}),"instanceName":"1"}),"instanceName":"1"}),"instanceName":"1"});
            var Q491;
            Q491=makeQuery(id+"F11.opPattern","COPY",BODY,{"derivedFrom":makeQuery(id+"F9.opPattern","COPY",BODY,{"derivedFrom":makeQuery(id+"F6.opPattern","COPY",BODY,{"derivedFrom":makeQuery(id+"F1.opRevolve","SWEPT_BODY",BODY,{"disambiguationData":[OSD([sQuery(id+"F0.wireOp",EDGE,"E1")])]}),"instanceName":"1"}),"instanceName":"1"}),"instanceName":"1"});
            var Q492;
            Q492=makeQuery(id+"F11.opPattern","COPY",BODY,{"derivedFrom":makeQuery(id+"F9.opPattern","COPY",BODY,{"derivedFrom":makeQuery(id+"F6.opPattern","COPY",BODY,{"derivedFrom":makeQuery(id+"F2.opPattern","COPY",BODY,{"derivedFrom":makeQuery(id+"F1.opRevolve","SWEPT_BODY",BODY,{"disambiguationData":[OSD([sQuery(id+"F0.wireOp",EDGE,"E1")])]}),"instanceName":"1"}),"instanceName":"1"}),"instanceName":"1"}),"instanceName":"1"});
            var Q493;
            Q493=makeQuery(id+"F11.opPattern","COPY",BODY,{"derivedFrom":makeQuery(id+"F9.opPattern","COPY",BODY,{"derivedFrom":makeQuery(id+"F6.opPattern","COPY",BODY,{"derivedFrom":makeQuery(id+"F3.opPattern","COPY",BODY,{"derivedFrom":makeQuery(id+"F2.opPattern","COPY",BODY,{"derivedFrom":makeQuery(id+"F1.opRevolve","SWEPT_BODY",BODY,{"disambiguationData":[OSD([sQuery(id+"F0.wireOp",EDGE,"E1")])]}),"instanceName":"1"}),"instanceName":"1"}),"instanceName":"1"}),"instanceName":"1"}),"instanceName":"1"});
            var Q494;
            Q494=makeQuery(id+"F11.opPattern","COPY",BODY,{"derivedFrom":makeQuery(id+"F9.opPattern","COPY",BODY,{"derivedFrom":makeQuery(id+"F6.opPattern","COPY",BODY,{"derivedFrom":makeQuery(id+"F4.opPattern","COPY",BODY,{"derivedFrom":makeQuery(id+"F1.opRevolve","SWEPT_BODY",BODY,{"disambiguationData":[OSD([sQuery(id+"F0.wireOp",EDGE,"E1")])]}),"instanceName":"1"}),"instanceName":"1"}),"instanceName":"1"}),"instanceName":"1"});
            var Q495;
            Q495=makeQuery(id+"F11.opPattern","COPY",BODY,{"derivedFrom":makeQuery(id+"F9.opPattern","COPY",BODY,{"derivedFrom":makeQuery(id+"F6.opPattern","COPY",BODY,{"derivedFrom":makeQuery(id+"F4.opPattern","COPY",BODY,{"derivedFrom":makeQuery(id+"F2.opPattern","COPY",BODY,{"derivedFrom":makeQuery(id+"F1.opRevolve","SWEPT_BODY",BODY,{"disambiguationData":[OSD([sQuery(id+"F0.wireOp",EDGE,"E1")])]}),"instanceName":"1"}),"instanceName":"1"}),"instanceName":"1"}),"instanceName":"1"}),"instanceName":"1"});
            var Q496;
            Q496=makeQuery(id+"F11.opPattern","COPY",BODY,{"derivedFrom":makeQuery(id+"F9.opPattern","COPY",BODY,{"derivedFrom":makeQuery(id+"F6.opPattern","COPY",BODY,{"derivedFrom":makeQuery(id+"F4.opPattern","COPY",BODY,{"derivedFrom":makeQuery(id+"F3.opPattern","COPY",BODY,{"derivedFrom":makeQuery(id+"F2.opPattern","COPY",BODY,{"derivedFrom":makeQuery(id+"F1.opRevolve","SWEPT_BODY",BODY,{"disambiguationData":[OSD([sQuery(id+"F0.wireOp",EDGE,"E1")])]}),"instanceName":"1"}),"instanceName":"1"}),"instanceName":"1"}),"instanceName":"1"}),"instanceName":"1"}),"instanceName":"1"});
            var Q497;
            Q497=makeQuery(id+"F11.opPattern","COPY",BODY,{"derivedFrom":makeQuery(id+"F9.opPattern","COPY",BODY,{"derivedFrom":makeQuery(id+"F6.opPattern","COPY",BODY,{"derivedFrom":makeQuery(id+"F5.opPattern","COPY",BODY,{"derivedFrom":makeQuery(id+"F1.opRevolve","SWEPT_BODY",BODY,{"disambiguationData":[OSD([sQuery(id+"F0.wireOp",EDGE,"E1")])]}),"instanceName":"1"}),"instanceName":"1"}),"instanceName":"1"}),"instanceName":"1"});
            var Q498;
            Q498=makeQuery(id+"F11.opPattern","COPY",BODY,{"derivedFrom":makeQuery(id+"F9.opPattern","COPY",BODY,{"derivedFrom":makeQuery(id+"F6.opPattern","COPY",BODY,{"derivedFrom":makeQuery(id+"F5.opPattern","COPY",BODY,{"derivedFrom":makeQuery(id+"F2.opPattern","COPY",BODY,{"derivedFrom":makeQuery(id+"F1.opRevolve","SWEPT_BODY",BODY,{"disambiguationData":[OSD([sQuery(id+"F0.wireOp",EDGE,"E1")])]}),"instanceName":"1"}),"instanceName":"1"}),"instanceName":"1"}),"instanceName":"1"}),"instanceName":"1"});
            var Q499;
            Q499=makeQuery(id+"F11.opPattern","COPY",BODY,{"derivedFrom":makeQuery(id+"F9.opPattern","COPY",BODY,{"derivedFrom":makeQuery(id+"F6.opPattern","COPY",BODY,{"derivedFrom":makeQuery(id+"F5.opPattern","COPY",BODY,{"derivedFrom":makeQuery(id+"F3.opPattern","COPY",BODY,{"derivedFrom":makeQuery(id+"F2.opPattern","COPY",BODY,{"derivedFrom":makeQuery(id+"F1.opRevolve","SWEPT_BODY",BODY,{"disambiguationData":[OSD([sQuery(id+"F0.wireOp",EDGE,"E1")])]}),"instanceName":"1"}),"instanceName":"1"}),"instanceName":"1"}),"instanceName":"1"}),"instanceName":"1"}),"instanceName":"1"});
            var Q500;
            Q500=makeQuery(id+"F11.opPattern","COPY",BODY,{"derivedFrom":makeQuery(id+"F9.opPattern","COPY",BODY,{"derivedFrom":makeQuery(id+"F6.opPattern","COPY",BODY,{"derivedFrom":makeQuery(id+"F5.opPattern","COPY",BODY,{"derivedFrom":makeQuery(id+"F4.opPattern","COPY",BODY,{"derivedFrom":makeQuery(id+"F1.opRevolve","SWEPT_BODY",BODY,{"disambiguationData":[OSD([sQuery(id+"F0.wireOp",EDGE,"E1")])]}),"instanceName":"1"}),"instanceName":"1"}),"instanceName":"1"}),"instanceName":"1"}),"instanceName":"1"});
            var Q501;
            Q501=makeQuery(id+"F11.opPattern","COPY",BODY,{"derivedFrom":makeQuery(id+"F9.opPattern","COPY",BODY,{"derivedFrom":makeQuery(id+"F6.opPattern","COPY",BODY,{"derivedFrom":makeQuery(id+"F5.opPattern","COPY",BODY,{"derivedFrom":makeQuery(id+"F4.opPattern","COPY",BODY,{"derivedFrom":makeQuery(id+"F2.opPattern","COPY",BODY,{"derivedFrom":makeQuery(id+"F1.opRevolve","SWEPT_BODY",BODY,{"disambiguationData":[OSD([sQuery(id+"F0.wireOp",EDGE,"E1")])]}),"instanceName":"1"}),"instanceName":"1"}),"instanceName":"1"}),"instanceName":"1"}),"instanceName":"1"}),"instanceName":"1"});
            var Q502;
            Q502=makeQuery(id+"F11.opPattern","COPY",BODY,{"derivedFrom":makeQuery(id+"F9.opPattern","COPY",BODY,{"derivedFrom":makeQuery(id+"F6.opPattern","COPY",BODY,{"derivedFrom":makeQuery(id+"F5.opPattern","COPY",BODY,{"derivedFrom":makeQuery(id+"F4.opPattern","COPY",BODY,{"derivedFrom":makeQuery(id+"F3.opPattern","COPY",BODY,{"derivedFrom":makeQuery(id+"F2.opPattern","COPY",BODY,{"derivedFrom":makeQuery(id+"F1.opRevolve","SWEPT_BODY",BODY,{"disambiguationData":[OSD([sQuery(id+"F0.wireOp",EDGE,"E1")])]}),"instanceName":"1"}),"instanceName":"1"}),"instanceName":"1"}),"instanceName":"1"}),"instanceName":"1"}),"instanceName":"1"}),"instanceName":"1"});
            var Q503;
            Q503=makeQuery(id+"F11.opPattern","COPY",BODY,{"derivedFrom":makeQuery(id+"F9.opPattern","COPY",BODY,{"derivedFrom":makeQuery(id+"F7.opPattern","COPY",BODY,{"derivedFrom":makeQuery(id+"F1.opRevolve","SWEPT_BODY",BODY,{"disambiguationData":[OSD([sQuery(id+"F0.wireOp",EDGE,"E1")])]}),"instanceName":"1"}),"instanceName":"1"}),"instanceName":"1"});
            var Q504;
            Q504=makeQuery(id+"F11.opPattern","COPY",BODY,{"derivedFrom":makeQuery(id+"F9.opPattern","COPY",BODY,{"derivedFrom":makeQuery(id+"F7.opPattern","COPY",BODY,{"derivedFrom":makeQuery(id+"F2.opPattern","COPY",BODY,{"derivedFrom":makeQuery(id+"F1.opRevolve","SWEPT_BODY",BODY,{"disambiguationData":[OSD([sQuery(id+"F0.wireOp",EDGE,"E1")])]}),"instanceName":"1"}),"instanceName":"1"}),"instanceName":"1"}),"instanceName":"1"});
            var Q505;
            Q505=makeQuery(id+"F11.opPattern","COPY",BODY,{"derivedFrom":makeQuery(id+"F9.opPattern","COPY",BODY,{"derivedFrom":makeQuery(id+"F7.opPattern","COPY",BODY,{"derivedFrom":makeQuery(id+"F3.opPattern","COPY",BODY,{"derivedFrom":makeQuery(id+"F2.opPattern","COPY",BODY,{"derivedFrom":makeQuery(id+"F1.opRevolve","SWEPT_BODY",BODY,{"disambiguationData":[OSD([sQuery(id+"F0.wireOp",EDGE,"E1")])]}),"instanceName":"1"}),"instanceName":"1"}),"instanceName":"1"}),"instanceName":"1"}),"instanceName":"1"});
            var Q506;
            Q506=makeQuery(id+"F11.opPattern","COPY",BODY,{"derivedFrom":makeQuery(id+"F9.opPattern","COPY",BODY,{"derivedFrom":makeQuery(id+"F7.opPattern","COPY",BODY,{"derivedFrom":makeQuery(id+"F4.opPattern","COPY",BODY,{"derivedFrom":makeQuery(id+"F1.opRevolve","SWEPT_BODY",BODY,{"disambiguationData":[OSD([sQuery(id+"F0.wireOp",EDGE,"E1")])]}),"instanceName":"1"}),"instanceName":"1"}),"instanceName":"1"}),"instanceName":"1"});
            var Q507;
            Q507=makeQuery(id+"F11.opPattern","COPY",BODY,{"derivedFrom":makeQuery(id+"F9.opPattern","COPY",BODY,{"derivedFrom":makeQuery(id+"F7.opPattern","COPY",BODY,{"derivedFrom":makeQuery(id+"F4.opPattern","COPY",BODY,{"derivedFrom":makeQuery(id+"F2.opPattern","COPY",BODY,{"derivedFrom":makeQuery(id+"F1.opRevolve","SWEPT_BODY",BODY,{"disambiguationData":[OSD([sQuery(id+"F0.wireOp",EDGE,"E1")])]}),"instanceName":"1"}),"instanceName":"1"}),"instanceName":"1"}),"instanceName":"1"}),"instanceName":"1"});
            var Q508;
            Q508=makeQuery(id+"F11.opPattern","COPY",BODY,{"derivedFrom":makeQuery(id+"F9.opPattern","COPY",BODY,{"derivedFrom":makeQuery(id+"F7.opPattern","COPY",BODY,{"derivedFrom":makeQuery(id+"F4.opPattern","COPY",BODY,{"derivedFrom":makeQuery(id+"F3.opPattern","COPY",BODY,{"derivedFrom":makeQuery(id+"F2.opPattern","COPY",BODY,{"derivedFrom":makeQuery(id+"F1.opRevolve","SWEPT_BODY",BODY,{"disambiguationData":[OSD([sQuery(id+"F0.wireOp",EDGE,"E1")])]}),"instanceName":"1"}),"instanceName":"1"}),"instanceName":"1"}),"instanceName":"1"}),"instanceName":"1"}),"instanceName":"1"});
            var Q509;
            Q509=makeQuery(id+"F11.opPattern","COPY",BODY,{"derivedFrom":makeQuery(id+"F9.opPattern","COPY",BODY,{"derivedFrom":makeQuery(id+"F7.opPattern","COPY",BODY,{"derivedFrom":makeQuery(id+"F5.opPattern","COPY",BODY,{"derivedFrom":makeQuery(id+"F1.opRevolve","SWEPT_BODY",BODY,{"disambiguationData":[OSD([sQuery(id+"F0.wireOp",EDGE,"E1")])]}),"instanceName":"1"}),"instanceName":"1"}),"instanceName":"1"}),"instanceName":"1"});
            var Q510;
            Q510=makeQuery(id+"F11.opPattern","COPY",BODY,{"derivedFrom":makeQuery(id+"F9.opPattern","COPY",BODY,{"derivedFrom":makeQuery(id+"F7.opPattern","COPY",BODY,{"derivedFrom":makeQuery(id+"F5.opPattern","COPY",BODY,{"derivedFrom":makeQuery(id+"F2.opPattern","COPY",BODY,{"derivedFrom":makeQuery(id+"F1.opRevolve","SWEPT_BODY",BODY,{"disambiguationData":[OSD([sQuery(id+"F0.wireOp",EDGE,"E1")])]}),"instanceName":"1"}),"instanceName":"1"}),"instanceName":"1"}),"instanceName":"1"}),"instanceName":"1"});
            var Q511;
            Q511=makeQuery(id+"F11.opPattern","COPY",BODY,{"derivedFrom":makeQuery(id+"F9.opPattern","COPY",BODY,{"derivedFrom":makeQuery(id+"F7.opPattern","COPY",BODY,{"derivedFrom":makeQuery(id+"F5.opPattern","COPY",BODY,{"derivedFrom":makeQuery(id+"F3.opPattern","COPY",BODY,{"derivedFrom":makeQuery(id+"F2.opPattern","COPY",BODY,{"derivedFrom":makeQuery(id+"F1.opRevolve","SWEPT_BODY",BODY,{"disambiguationData":[OSD([sQuery(id+"F0.wireOp",EDGE,"E1")])]}),"instanceName":"1"}),"instanceName":"1"}),"instanceName":"1"}),"instanceName":"1"}),"instanceName":"1"}),"instanceName":"1"});
            var Q512;
            Q512=makeQuery(id+"F11.opPattern","COPY",BODY,{"derivedFrom":makeQuery(id+"F9.opPattern","COPY",BODY,{"derivedFrom":makeQuery(id+"F7.opPattern","COPY",BODY,{"derivedFrom":makeQuery(id+"F5.opPattern","COPY",BODY,{"derivedFrom":makeQuery(id+"F4.opPattern","COPY",BODY,{"derivedFrom":makeQuery(id+"F1.opRevolve","SWEPT_BODY",BODY,{"disambiguationData":[OSD([sQuery(id+"F0.wireOp",EDGE,"E1")])]}),"instanceName":"1"}),"instanceName":"1"}),"instanceName":"1"}),"instanceName":"1"}),"instanceName":"1"});
            var Q513;
            Q513=makeQuery(id+"F11.opPattern","COPY",BODY,{"derivedFrom":makeQuery(id+"F9.opPattern","COPY",BODY,{"derivedFrom":makeQuery(id+"F7.opPattern","COPY",BODY,{"derivedFrom":makeQuery(id+"F5.opPattern","COPY",BODY,{"derivedFrom":makeQuery(id+"F4.opPattern","COPY",BODY,{"derivedFrom":makeQuery(id+"F2.opPattern","COPY",BODY,{"derivedFrom":makeQuery(id+"F1.opRevolve","SWEPT_BODY",BODY,{"disambiguationData":[OSD([sQuery(id+"F0.wireOp",EDGE,"E1")])]}),"instanceName":"1"}),"instanceName":"1"}),"instanceName":"1"}),"instanceName":"1"}),"instanceName":"1"}),"instanceName":"1"});
            var Q514;
            Q514=makeQuery(id+"F11.opPattern","COPY",BODY,{"derivedFrom":makeQuery(id+"F9.opPattern","COPY",BODY,{"derivedFrom":makeQuery(id+"F7.opPattern","COPY",BODY,{"derivedFrom":makeQuery(id+"F5.opPattern","COPY",BODY,{"derivedFrom":makeQuery(id+"F4.opPattern","COPY",BODY,{"derivedFrom":makeQuery(id+"F3.opPattern","COPY",BODY,{"derivedFrom":makeQuery(id+"F2.opPattern","COPY",BODY,{"derivedFrom":makeQuery(id+"F1.opRevolve","SWEPT_BODY",BODY,{"disambiguationData":[OSD([sQuery(id+"F0.wireOp",EDGE,"E1")])]}),"instanceName":"1"}),"instanceName":"1"}),"instanceName":"1"}),"instanceName":"1"}),"instanceName":"1"}),"instanceName":"1"}),"instanceName":"1"});
            var Q515;
            Q515=makeQuery(id+"F11.opPattern","COPY",BODY,{"derivedFrom":makeQuery(id+"F9.opPattern","COPY",BODY,{"derivedFrom":makeQuery(id+"F7.opPattern","COPY",BODY,{"derivedFrom":makeQuery(id+"F6.opPattern","COPY",BODY,{"derivedFrom":makeQuery(id+"F1.opRevolve","SWEPT_BODY",BODY,{"disambiguationData":[OSD([sQuery(id+"F0.wireOp",EDGE,"E1")])]}),"instanceName":"1"}),"instanceName":"1"}),"instanceName":"1"}),"instanceName":"1"});
            var Q516;
            Q516=makeQuery(id+"F11.opPattern","COPY",BODY,{"derivedFrom":makeQuery(id+"F9.opPattern","COPY",BODY,{"derivedFrom":makeQuery(id+"F7.opPattern","COPY",BODY,{"derivedFrom":makeQuery(id+"F6.opPattern","COPY",BODY,{"derivedFrom":makeQuery(id+"F2.opPattern","COPY",BODY,{"derivedFrom":makeQuery(id+"F1.opRevolve","SWEPT_BODY",BODY,{"disambiguationData":[OSD([sQuery(id+"F0.wireOp",EDGE,"E1")])]}),"instanceName":"1"}),"instanceName":"1"}),"instanceName":"1"}),"instanceName":"1"}),"instanceName":"1"});
            var Q517;
            Q517=makeQuery(id+"F11.opPattern","COPY",BODY,{"derivedFrom":makeQuery(id+"F9.opPattern","COPY",BODY,{"derivedFrom":makeQuery(id+"F7.opPattern","COPY",BODY,{"derivedFrom":makeQuery(id+"F6.opPattern","COPY",BODY,{"derivedFrom":makeQuery(id+"F3.opPattern","COPY",BODY,{"derivedFrom":makeQuery(id+"F2.opPattern","COPY",BODY,{"derivedFrom":makeQuery(id+"F1.opRevolve","SWEPT_BODY",BODY,{"disambiguationData":[OSD([sQuery(id+"F0.wireOp",EDGE,"E1")])]}),"instanceName":"1"}),"instanceName":"1"}),"instanceName":"1"}),"instanceName":"1"}),"instanceName":"1"}),"instanceName":"1"});
            var Q518;
            Q518=makeQuery(id+"F11.opPattern","COPY",BODY,{"derivedFrom":makeQuery(id+"F9.opPattern","COPY",BODY,{"derivedFrom":makeQuery(id+"F7.opPattern","COPY",BODY,{"derivedFrom":makeQuery(id+"F6.opPattern","COPY",BODY,{"derivedFrom":makeQuery(id+"F4.opPattern","COPY",BODY,{"derivedFrom":makeQuery(id+"F1.opRevolve","SWEPT_BODY",BODY,{"disambiguationData":[OSD([sQuery(id+"F0.wireOp",EDGE,"E1")])]}),"instanceName":"1"}),"instanceName":"1"}),"instanceName":"1"}),"instanceName":"1"}),"instanceName":"1"});
            var Q519;
            Q519=makeQuery(id+"F11.opPattern","COPY",BODY,{"derivedFrom":makeQuery(id+"F9.opPattern","COPY",BODY,{"derivedFrom":makeQuery(id+"F7.opPattern","COPY",BODY,{"derivedFrom":makeQuery(id+"F6.opPattern","COPY",BODY,{"derivedFrom":makeQuery(id+"F4.opPattern","COPY",BODY,{"derivedFrom":makeQuery(id+"F2.opPattern","COPY",BODY,{"derivedFrom":makeQuery(id+"F1.opRevolve","SWEPT_BODY",BODY,{"disambiguationData":[OSD([sQuery(id+"F0.wireOp",EDGE,"E1")])]}),"instanceName":"1"}),"instanceName":"1"}),"instanceName":"1"}),"instanceName":"1"}),"instanceName":"1"}),"instanceName":"1"});
            var Q520;
            Q520=makeQuery(id+"F11.opPattern","COPY",BODY,{"derivedFrom":makeQuery(id+"F9.opPattern","COPY",BODY,{"derivedFrom":makeQuery(id+"F7.opPattern","COPY",BODY,{"derivedFrom":makeQuery(id+"F6.opPattern","COPY",BODY,{"derivedFrom":makeQuery(id+"F4.opPattern","COPY",BODY,{"derivedFrom":makeQuery(id+"F3.opPattern","COPY",BODY,{"derivedFrom":makeQuery(id+"F2.opPattern","COPY",BODY,{"derivedFrom":makeQuery(id+"F1.opRevolve","SWEPT_BODY",BODY,{"disambiguationData":[OSD([sQuery(id+"F0.wireOp",EDGE,"E1")])]}),"instanceName":"1"}),"instanceName":"1"}),"instanceName":"1"}),"instanceName":"1"}),"instanceName":"1"}),"instanceName":"1"}),"instanceName":"1"});
            var Q521;
            Q521=makeQuery(id+"F11.opPattern","COPY",BODY,{"derivedFrom":makeQuery(id+"F9.opPattern","COPY",BODY,{"derivedFrom":makeQuery(id+"F7.opPattern","COPY",BODY,{"derivedFrom":makeQuery(id+"F6.opPattern","COPY",BODY,{"derivedFrom":makeQuery(id+"F5.opPattern","COPY",BODY,{"derivedFrom":makeQuery(id+"F1.opRevolve","SWEPT_BODY",BODY,{"disambiguationData":[OSD([sQuery(id+"F0.wireOp",EDGE,"E1")])]}),"instanceName":"1"}),"instanceName":"1"}),"instanceName":"1"}),"instanceName":"1"}),"instanceName":"1"});
            var Q522;
            Q522=makeQuery(id+"F11.opPattern","COPY",BODY,{"derivedFrom":makeQuery(id+"F9.opPattern","COPY",BODY,{"derivedFrom":makeQuery(id+"F7.opPattern","COPY",BODY,{"derivedFrom":makeQuery(id+"F6.opPattern","COPY",BODY,{"derivedFrom":makeQuery(id+"F5.opPattern","COPY",BODY,{"derivedFrom":makeQuery(id+"F2.opPattern","COPY",BODY,{"derivedFrom":makeQuery(id+"F1.opRevolve","SWEPT_BODY",BODY,{"disambiguationData":[OSD([sQuery(id+"F0.wireOp",EDGE,"E1")])]}),"instanceName":"1"}),"instanceName":"1"}),"instanceName":"1"}),"instanceName":"1"}),"instanceName":"1"}),"instanceName":"1"});
            var Q523;
            Q523=makeQuery(id+"F11.opPattern","COPY",BODY,{"derivedFrom":makeQuery(id+"F9.opPattern","COPY",BODY,{"derivedFrom":makeQuery(id+"F7.opPattern","COPY",BODY,{"derivedFrom":makeQuery(id+"F6.opPattern","COPY",BODY,{"derivedFrom":makeQuery(id+"F5.opPattern","COPY",BODY,{"derivedFrom":makeQuery(id+"F3.opPattern","COPY",BODY,{"derivedFrom":makeQuery(id+"F2.opPattern","COPY",BODY,{"derivedFrom":makeQuery(id+"F1.opRevolve","SWEPT_BODY",BODY,{"disambiguationData":[OSD([sQuery(id+"F0.wireOp",EDGE,"E1")])]}),"instanceName":"1"}),"instanceName":"1"}),"instanceName":"1"}),"instanceName":"1"}),"instanceName":"1"}),"instanceName":"1"}),"instanceName":"1"});
            var Q524;
            Q524=makeQuery(id+"F11.opPattern","COPY",BODY,{"derivedFrom":makeQuery(id+"F9.opPattern","COPY",BODY,{"derivedFrom":makeQuery(id+"F7.opPattern","COPY",BODY,{"derivedFrom":makeQuery(id+"F6.opPattern","COPY",BODY,{"derivedFrom":makeQuery(id+"F5.opPattern","COPY",BODY,{"derivedFrom":makeQuery(id+"F4.opPattern","COPY",BODY,{"derivedFrom":makeQuery(id+"F1.opRevolve","SWEPT_BODY",BODY,{"disambiguationData":[OSD([sQuery(id+"F0.wireOp",EDGE,"E1")])]}),"instanceName":"1"}),"instanceName":"1"}),"instanceName":"1"}),"instanceName":"1"}),"instanceName":"1"}),"instanceName":"1"});
            var Q525;
            Q525=makeQuery(id+"F11.opPattern","COPY",BODY,{"derivedFrom":makeQuery(id+"F9.opPattern","COPY",BODY,{"derivedFrom":makeQuery(id+"F7.opPattern","COPY",BODY,{"derivedFrom":makeQuery(id+"F6.opPattern","COPY",BODY,{"derivedFrom":makeQuery(id+"F5.opPattern","COPY",BODY,{"derivedFrom":makeQuery(id+"F4.opPattern","COPY",BODY,{"derivedFrom":makeQuery(id+"F2.opPattern","COPY",BODY,{"derivedFrom":makeQuery(id+"F1.opRevolve","SWEPT_BODY",BODY,{"disambiguationData":[OSD([sQuery(id+"F0.wireOp",EDGE,"E1")])]}),"instanceName":"1"}),"instanceName":"1"}),"instanceName":"1"}),"instanceName":"1"}),"instanceName":"1"}),"instanceName":"1"}),"instanceName":"1"});
            var Q526;
            Q526=makeQuery(id+"F11.opPattern","COPY",BODY,{"derivedFrom":makeQuery(id+"F9.opPattern","COPY",BODY,{"derivedFrom":makeQuery(id+"F7.opPattern","COPY",BODY,{"derivedFrom":makeQuery(id+"F6.opPattern","COPY",BODY,{"derivedFrom":makeQuery(id+"F5.opPattern","COPY",BODY,{"derivedFrom":makeQuery(id+"F4.opPattern","COPY",BODY,{"derivedFrom":makeQuery(id+"F3.opPattern","COPY",BODY,{"derivedFrom":makeQuery(id+"F2.opPattern","COPY",BODY,{"derivedFrom":makeQuery(id+"F1.opRevolve","SWEPT_BODY",BODY,{"disambiguationData":[OSD([sQuery(id+"F0.wireOp",EDGE,"E1")])]}),"instanceName":"1"}),"instanceName":"1"}),"instanceName":"1"}),"instanceName":"1"}),"instanceName":"1"}),"instanceName":"1"}),"instanceName":"1"}),"instanceName":"1"});
            var Q527;
            Q527=makeQuery(id+"F11.opPattern","COPY",BODY,{"derivedFrom":makeQuery(id+"F9.opPattern","COPY",BODY,{"derivedFrom":makeQuery(id+"F8.opPattern","COPY",BODY,{"derivedFrom":makeQuery(id+"F1.opRevolve","SWEPT_BODY",BODY,{"disambiguationData":[OSD([sQuery(id+"F0.wireOp",EDGE,"E1")])]}),"instanceName":"1"}),"instanceName":"1"}),"instanceName":"1"});
            var Q528;
            Q528=makeQuery(id+"F11.opPattern","COPY",BODY,{"derivedFrom":makeQuery(id+"F9.opPattern","COPY",BODY,{"derivedFrom":makeQuery(id+"F8.opPattern","COPY",BODY,{"derivedFrom":makeQuery(id+"F2.opPattern","COPY",BODY,{"derivedFrom":makeQuery(id+"F1.opRevolve","SWEPT_BODY",BODY,{"disambiguationData":[OSD([sQuery(id+"F0.wireOp",EDGE,"E1")])]}),"instanceName":"1"}),"instanceName":"1"}),"instanceName":"1"}),"instanceName":"1"});
            var Q529;
            Q529=makeQuery(id+"F11.opPattern","COPY",BODY,{"derivedFrom":makeQuery(id+"F9.opPattern","COPY",BODY,{"derivedFrom":makeQuery(id+"F8.opPattern","COPY",BODY,{"derivedFrom":makeQuery(id+"F3.opPattern","COPY",BODY,{"derivedFrom":makeQuery(id+"F2.opPattern","COPY",BODY,{"derivedFrom":makeQuery(id+"F1.opRevolve","SWEPT_BODY",BODY,{"disambiguationData":[OSD([sQuery(id+"F0.wireOp",EDGE,"E1")])]}),"instanceName":"1"}),"instanceName":"1"}),"instanceName":"1"}),"instanceName":"1"}),"instanceName":"1"});
            var Q530;
            Q530=makeQuery(id+"F11.opPattern","COPY",BODY,{"derivedFrom":makeQuery(id+"F9.opPattern","COPY",BODY,{"derivedFrom":makeQuery(id+"F8.opPattern","COPY",BODY,{"derivedFrom":makeQuery(id+"F4.opPattern","COPY",BODY,{"derivedFrom":makeQuery(id+"F1.opRevolve","SWEPT_BODY",BODY,{"disambiguationData":[OSD([sQuery(id+"F0.wireOp",EDGE,"E1")])]}),"instanceName":"1"}),"instanceName":"1"}),"instanceName":"1"}),"instanceName":"1"});
            var Q531;
            Q531=makeQuery(id+"F11.opPattern","COPY",BODY,{"derivedFrom":makeQuery(id+"F9.opPattern","COPY",BODY,{"derivedFrom":makeQuery(id+"F8.opPattern","COPY",BODY,{"derivedFrom":makeQuery(id+"F4.opPattern","COPY",BODY,{"derivedFrom":makeQuery(id+"F2.opPattern","COPY",BODY,{"derivedFrom":makeQuery(id+"F1.opRevolve","SWEPT_BODY",BODY,{"disambiguationData":[OSD([sQuery(id+"F0.wireOp",EDGE,"E1")])]}),"instanceName":"1"}),"instanceName":"1"}),"instanceName":"1"}),"instanceName":"1"}),"instanceName":"1"});
            var Q532;
            Q532=makeQuery(id+"F11.opPattern","COPY",BODY,{"derivedFrom":makeQuery(id+"F9.opPattern","COPY",BODY,{"derivedFrom":makeQuery(id+"F8.opPattern","COPY",BODY,{"derivedFrom":makeQuery(id+"F4.opPattern","COPY",BODY,{"derivedFrom":makeQuery(id+"F3.opPattern","COPY",BODY,{"derivedFrom":makeQuery(id+"F2.opPattern","COPY",BODY,{"derivedFrom":makeQuery(id+"F1.opRevolve","SWEPT_BODY",BODY,{"disambiguationData":[OSD([sQuery(id+"F0.wireOp",EDGE,"E1")])]}),"instanceName":"1"}),"instanceName":"1"}),"instanceName":"1"}),"instanceName":"1"}),"instanceName":"1"}),"instanceName":"1"});
            var Q533;
            Q533=makeQuery(id+"F11.opPattern","COPY",BODY,{"derivedFrom":makeQuery(id+"F9.opPattern","COPY",BODY,{"derivedFrom":makeQuery(id+"F8.opPattern","COPY",BODY,{"derivedFrom":makeQuery(id+"F5.opPattern","COPY",BODY,{"derivedFrom":makeQuery(id+"F1.opRevolve","SWEPT_BODY",BODY,{"disambiguationData":[OSD([sQuery(id+"F0.wireOp",EDGE,"E1")])]}),"instanceName":"1"}),"instanceName":"1"}),"instanceName":"1"}),"instanceName":"1"});
            var Q534;
            Q534=makeQuery(id+"F11.opPattern","COPY",BODY,{"derivedFrom":makeQuery(id+"F9.opPattern","COPY",BODY,{"derivedFrom":makeQuery(id+"F8.opPattern","COPY",BODY,{"derivedFrom":makeQuery(id+"F5.opPattern","COPY",BODY,{"derivedFrom":makeQuery(id+"F2.opPattern","COPY",BODY,{"derivedFrom":makeQuery(id+"F1.opRevolve","SWEPT_BODY",BODY,{"disambiguationData":[OSD([sQuery(id+"F0.wireOp",EDGE,"E1")])]}),"instanceName":"1"}),"instanceName":"1"}),"instanceName":"1"}),"instanceName":"1"}),"instanceName":"1"});
            var Q535;
            Q535=makeQuery(id+"F11.opPattern","COPY",BODY,{"derivedFrom":makeQuery(id+"F9.opPattern","COPY",BODY,{"derivedFrom":makeQuery(id+"F8.opPattern","COPY",BODY,{"derivedFrom":makeQuery(id+"F5.opPattern","COPY",BODY,{"derivedFrom":makeQuery(id+"F3.opPattern","COPY",BODY,{"derivedFrom":makeQuery(id+"F2.opPattern","COPY",BODY,{"derivedFrom":makeQuery(id+"F1.opRevolve","SWEPT_BODY",BODY,{"disambiguationData":[OSD([sQuery(id+"F0.wireOp",EDGE,"E1")])]}),"instanceName":"1"}),"instanceName":"1"}),"instanceName":"1"}),"instanceName":"1"}),"instanceName":"1"}),"instanceName":"1"});
            var Q536;
            Q536=makeQuery(id+"F11.opPattern","COPY",BODY,{"derivedFrom":makeQuery(id+"F9.opPattern","COPY",BODY,{"derivedFrom":makeQuery(id+"F8.opPattern","COPY",BODY,{"derivedFrom":makeQuery(id+"F5.opPattern","COPY",BODY,{"derivedFrom":makeQuery(id+"F4.opPattern","COPY",BODY,{"derivedFrom":makeQuery(id+"F1.opRevolve","SWEPT_BODY",BODY,{"disambiguationData":[OSD([sQuery(id+"F0.wireOp",EDGE,"E1")])]}),"instanceName":"1"}),"instanceName":"1"}),"instanceName":"1"}),"instanceName":"1"}),"instanceName":"1"});
            var Q537;
            Q537=makeQuery(id+"F11.opPattern","COPY",BODY,{"derivedFrom":makeQuery(id+"F9.opPattern","COPY",BODY,{"derivedFrom":makeQuery(id+"F8.opPattern","COPY",BODY,{"derivedFrom":makeQuery(id+"F5.opPattern","COPY",BODY,{"derivedFrom":makeQuery(id+"F4.opPattern","COPY",BODY,{"derivedFrom":makeQuery(id+"F2.opPattern","COPY",BODY,{"derivedFrom":makeQuery(id+"F1.opRevolve","SWEPT_BODY",BODY,{"disambiguationData":[OSD([sQuery(id+"F0.wireOp",EDGE,"E1")])]}),"instanceName":"1"}),"instanceName":"1"}),"instanceName":"1"}),"instanceName":"1"}),"instanceName":"1"}),"instanceName":"1"});
            var Q538;
            Q538=makeQuery(id+"F11.opPattern","COPY",BODY,{"derivedFrom":makeQuery(id+"F9.opPattern","COPY",BODY,{"derivedFrom":makeQuery(id+"F8.opPattern","COPY",BODY,{"derivedFrom":makeQuery(id+"F5.opPattern","COPY",BODY,{"derivedFrom":makeQuery(id+"F4.opPattern","COPY",BODY,{"derivedFrom":makeQuery(id+"F3.opPattern","COPY",BODY,{"derivedFrom":makeQuery(id+"F2.opPattern","COPY",BODY,{"derivedFrom":makeQuery(id+"F1.opRevolve","SWEPT_BODY",BODY,{"disambiguationData":[OSD([sQuery(id+"F0.wireOp",EDGE,"E1")])]}),"instanceName":"1"}),"instanceName":"1"}),"instanceName":"1"}),"instanceName":"1"}),"instanceName":"1"}),"instanceName":"1"}),"instanceName":"1"});
            var Q539;
            Q539=makeQuery(id+"F11.opPattern","COPY",BODY,{"derivedFrom":makeQuery(id+"F9.opPattern","COPY",BODY,{"derivedFrom":makeQuery(id+"F8.opPattern","COPY",BODY,{"derivedFrom":makeQuery(id+"F6.opPattern","COPY",BODY,{"derivedFrom":makeQuery(id+"F1.opRevolve","SWEPT_BODY",BODY,{"disambiguationData":[OSD([sQuery(id+"F0.wireOp",EDGE,"E1")])]}),"instanceName":"1"}),"instanceName":"1"}),"instanceName":"1"}),"instanceName":"1"});
            var Q540;
            Q540=makeQuery(id+"F11.opPattern","COPY",BODY,{"derivedFrom":makeQuery(id+"F9.opPattern","COPY",BODY,{"derivedFrom":makeQuery(id+"F8.opPattern","COPY",BODY,{"derivedFrom":makeQuery(id+"F6.opPattern","COPY",BODY,{"derivedFrom":makeQuery(id+"F2.opPattern","COPY",BODY,{"derivedFrom":makeQuery(id+"F1.opRevolve","SWEPT_BODY",BODY,{"disambiguationData":[OSD([sQuery(id+"F0.wireOp",EDGE,"E1")])]}),"instanceName":"1"}),"instanceName":"1"}),"instanceName":"1"}),"instanceName":"1"}),"instanceName":"1"});
            var Q541;
            Q541=makeQuery(id+"F11.opPattern","COPY",BODY,{"derivedFrom":makeQuery(id+"F9.opPattern","COPY",BODY,{"derivedFrom":makeQuery(id+"F8.opPattern","COPY",BODY,{"derivedFrom":makeQuery(id+"F6.opPattern","COPY",BODY,{"derivedFrom":makeQuery(id+"F3.opPattern","COPY",BODY,{"derivedFrom":makeQuery(id+"F2.opPattern","COPY",BODY,{"derivedFrom":makeQuery(id+"F1.opRevolve","SWEPT_BODY",BODY,{"disambiguationData":[OSD([sQuery(id+"F0.wireOp",EDGE,"E1")])]}),"instanceName":"1"}),"instanceName":"1"}),"instanceName":"1"}),"instanceName":"1"}),"instanceName":"1"}),"instanceName":"1"});
            var Q542;
            Q542=makeQuery(id+"F11.opPattern","COPY",BODY,{"derivedFrom":makeQuery(id+"F9.opPattern","COPY",BODY,{"derivedFrom":makeQuery(id+"F8.opPattern","COPY",BODY,{"derivedFrom":makeQuery(id+"F6.opPattern","COPY",BODY,{"derivedFrom":makeQuery(id+"F4.opPattern","COPY",BODY,{"derivedFrom":makeQuery(id+"F1.opRevolve","SWEPT_BODY",BODY,{"disambiguationData":[OSD([sQuery(id+"F0.wireOp",EDGE,"E1")])]}),"instanceName":"1"}),"instanceName":"1"}),"instanceName":"1"}),"instanceName":"1"}),"instanceName":"1"});
            var Q543;
            Q543=makeQuery(id+"F11.opPattern","COPY",BODY,{"derivedFrom":makeQuery(id+"F9.opPattern","COPY",BODY,{"derivedFrom":makeQuery(id+"F8.opPattern","COPY",BODY,{"derivedFrom":makeQuery(id+"F6.opPattern","COPY",BODY,{"derivedFrom":makeQuery(id+"F4.opPattern","COPY",BODY,{"derivedFrom":makeQuery(id+"F2.opPattern","COPY",BODY,{"derivedFrom":makeQuery(id+"F1.opRevolve","SWEPT_BODY",BODY,{"disambiguationData":[OSD([sQuery(id+"F0.wireOp",EDGE,"E1")])]}),"instanceName":"1"}),"instanceName":"1"}),"instanceName":"1"}),"instanceName":"1"}),"instanceName":"1"}),"instanceName":"1"});
            var Q544;
            Q544=makeQuery(id+"F11.opPattern","COPY",BODY,{"derivedFrom":makeQuery(id+"F9.opPattern","COPY",BODY,{"derivedFrom":makeQuery(id+"F8.opPattern","COPY",BODY,{"derivedFrom":makeQuery(id+"F6.opPattern","COPY",BODY,{"derivedFrom":makeQuery(id+"F4.opPattern","COPY",BODY,{"derivedFrom":makeQuery(id+"F3.opPattern","COPY",BODY,{"derivedFrom":makeQuery(id+"F2.opPattern","COPY",BODY,{"derivedFrom":makeQuery(id+"F1.opRevolve","SWEPT_BODY",BODY,{"disambiguationData":[OSD([sQuery(id+"F0.wireOp",EDGE,"E1")])]}),"instanceName":"1"}),"instanceName":"1"}),"instanceName":"1"}),"instanceName":"1"}),"instanceName":"1"}),"instanceName":"1"}),"instanceName":"1"});
            var Q545;
            Q545=makeQuery(id+"F11.opPattern","COPY",BODY,{"derivedFrom":makeQuery(id+"F9.opPattern","COPY",BODY,{"derivedFrom":makeQuery(id+"F8.opPattern","COPY",BODY,{"derivedFrom":makeQuery(id+"F6.opPattern","COPY",BODY,{"derivedFrom":makeQuery(id+"F5.opPattern","COPY",BODY,{"derivedFrom":makeQuery(id+"F1.opRevolve","SWEPT_BODY",BODY,{"disambiguationData":[OSD([sQuery(id+"F0.wireOp",EDGE,"E1")])]}),"instanceName":"1"}),"instanceName":"1"}),"instanceName":"1"}),"instanceName":"1"}),"instanceName":"1"});
            var Q546;
            Q546=makeQuery(id+"F11.opPattern","COPY",BODY,{"derivedFrom":makeQuery(id+"F9.opPattern","COPY",BODY,{"derivedFrom":makeQuery(id+"F8.opPattern","COPY",BODY,{"derivedFrom":makeQuery(id+"F6.opPattern","COPY",BODY,{"derivedFrom":makeQuery(id+"F5.opPattern","COPY",BODY,{"derivedFrom":makeQuery(id+"F2.opPattern","COPY",BODY,{"derivedFrom":makeQuery(id+"F1.opRevolve","SWEPT_BODY",BODY,{"disambiguationData":[OSD([sQuery(id+"F0.wireOp",EDGE,"E1")])]}),"instanceName":"1"}),"instanceName":"1"}),"instanceName":"1"}),"instanceName":"1"}),"instanceName":"1"}),"instanceName":"1"});
            var Q547;
            Q547=makeQuery(id+"F11.opPattern","COPY",BODY,{"derivedFrom":makeQuery(id+"F9.opPattern","COPY",BODY,{"derivedFrom":makeQuery(id+"F8.opPattern","COPY",BODY,{"derivedFrom":makeQuery(id+"F6.opPattern","COPY",BODY,{"derivedFrom":makeQuery(id+"F5.opPattern","COPY",BODY,{"derivedFrom":makeQuery(id+"F3.opPattern","COPY",BODY,{"derivedFrom":makeQuery(id+"F2.opPattern","COPY",BODY,{"derivedFrom":makeQuery(id+"F1.opRevolve","SWEPT_BODY",BODY,{"disambiguationData":[OSD([sQuery(id+"F0.wireOp",EDGE,"E1")])]}),"instanceName":"1"}),"instanceName":"1"}),"instanceName":"1"}),"instanceName":"1"}),"instanceName":"1"}),"instanceName":"1"}),"instanceName":"1"});
            var Q548;
            Q548=makeQuery(id+"F11.opPattern","COPY",BODY,{"derivedFrom":makeQuery(id+"F9.opPattern","COPY",BODY,{"derivedFrom":makeQuery(id+"F8.opPattern","COPY",BODY,{"derivedFrom":makeQuery(id+"F6.opPattern","COPY",BODY,{"derivedFrom":makeQuery(id+"F5.opPattern","COPY",BODY,{"derivedFrom":makeQuery(id+"F4.opPattern","COPY",BODY,{"derivedFrom":makeQuery(id+"F1.opRevolve","SWEPT_BODY",BODY,{"disambiguationData":[OSD([sQuery(id+"F0.wireOp",EDGE,"E1")])]}),"instanceName":"1"}),"instanceName":"1"}),"instanceName":"1"}),"instanceName":"1"}),"instanceName":"1"}),"instanceName":"1"});
            var Q549;
            Q549=makeQuery(id+"F11.opPattern","COPY",BODY,{"derivedFrom":makeQuery(id+"F9.opPattern","COPY",BODY,{"derivedFrom":makeQuery(id+"F8.opPattern","COPY",BODY,{"derivedFrom":makeQuery(id+"F6.opPattern","COPY",BODY,{"derivedFrom":makeQuery(id+"F5.opPattern","COPY",BODY,{"derivedFrom":makeQuery(id+"F4.opPattern","COPY",BODY,{"derivedFrom":makeQuery(id+"F2.opPattern","COPY",BODY,{"derivedFrom":makeQuery(id+"F1.opRevolve","SWEPT_BODY",BODY,{"disambiguationData":[OSD([sQuery(id+"F0.wireOp",EDGE,"E1")])]}),"instanceName":"1"}),"instanceName":"1"}),"instanceName":"1"}),"instanceName":"1"}),"instanceName":"1"}),"instanceName":"1"}),"instanceName":"1"});
            var Q550;
            Q550=makeQuery(id+"F11.opPattern","COPY",BODY,{"derivedFrom":makeQuery(id+"F9.opPattern","COPY",BODY,{"derivedFrom":makeQuery(id+"F8.opPattern","COPY",BODY,{"derivedFrom":makeQuery(id+"F6.opPattern","COPY",BODY,{"derivedFrom":makeQuery(id+"F5.opPattern","COPY",BODY,{"derivedFrom":makeQuery(id+"F4.opPattern","COPY",BODY,{"derivedFrom":makeQuery(id+"F3.opPattern","COPY",BODY,{"derivedFrom":makeQuery(id+"F2.opPattern","COPY",BODY,{"derivedFrom":makeQuery(id+"F1.opRevolve","SWEPT_BODY",BODY,{"disambiguationData":[OSD([sQuery(id+"F0.wireOp",EDGE,"E1")])]}),"instanceName":"1"}),"instanceName":"1"}),"instanceName":"1"}),"instanceName":"1"}),"instanceName":"1"}),"instanceName":"1"}),"instanceName":"1"}),"instanceName":"1"});
            var Q551;
            Q551=makeQuery(id+"F11.opPattern","COPY",BODY,{"derivedFrom":makeQuery(id+"F9.opPattern","COPY",BODY,{"derivedFrom":makeQuery(id+"F8.opPattern","COPY",BODY,{"derivedFrom":makeQuery(id+"F7.opPattern","COPY",BODY,{"derivedFrom":makeQuery(id+"F1.opRevolve","SWEPT_BODY",BODY,{"disambiguationData":[OSD([sQuery(id+"F0.wireOp",EDGE,"E1")])]}),"instanceName":"1"}),"instanceName":"1"}),"instanceName":"1"}),"instanceName":"1"});
            var Q552;
            Q552=makeQuery(id+"F11.opPattern","COPY",BODY,{"derivedFrom":makeQuery(id+"F9.opPattern","COPY",BODY,{"derivedFrom":makeQuery(id+"F8.opPattern","COPY",BODY,{"derivedFrom":makeQuery(id+"F7.opPattern","COPY",BODY,{"derivedFrom":makeQuery(id+"F2.opPattern","COPY",BODY,{"derivedFrom":makeQuery(id+"F1.opRevolve","SWEPT_BODY",BODY,{"disambiguationData":[OSD([sQuery(id+"F0.wireOp",EDGE,"E1")])]}),"instanceName":"1"}),"instanceName":"1"}),"instanceName":"1"}),"instanceName":"1"}),"instanceName":"1"});
            var Q553;
            Q553=makeQuery(id+"F11.opPattern","COPY",BODY,{"derivedFrom":makeQuery(id+"F9.opPattern","COPY",BODY,{"derivedFrom":makeQuery(id+"F8.opPattern","COPY",BODY,{"derivedFrom":makeQuery(id+"F7.opPattern","COPY",BODY,{"derivedFrom":makeQuery(id+"F3.opPattern","COPY",BODY,{"derivedFrom":makeQuery(id+"F2.opPattern","COPY",BODY,{"derivedFrom":makeQuery(id+"F1.opRevolve","SWEPT_BODY",BODY,{"disambiguationData":[OSD([sQuery(id+"F0.wireOp",EDGE,"E1")])]}),"instanceName":"1"}),"instanceName":"1"}),"instanceName":"1"}),"instanceName":"1"}),"instanceName":"1"}),"instanceName":"1"});
            var Q554;
            Q554=makeQuery(id+"F11.opPattern","COPY",BODY,{"derivedFrom":makeQuery(id+"F9.opPattern","COPY",BODY,{"derivedFrom":makeQuery(id+"F8.opPattern","COPY",BODY,{"derivedFrom":makeQuery(id+"F7.opPattern","COPY",BODY,{"derivedFrom":makeQuery(id+"F4.opPattern","COPY",BODY,{"derivedFrom":makeQuery(id+"F1.opRevolve","SWEPT_BODY",BODY,{"disambiguationData":[OSD([sQuery(id+"F0.wireOp",EDGE,"E1")])]}),"instanceName":"1"}),"instanceName":"1"}),"instanceName":"1"}),"instanceName":"1"}),"instanceName":"1"});
            var Q555;
            Q555=makeQuery(id+"F11.opPattern","COPY",BODY,{"derivedFrom":makeQuery(id+"F9.opPattern","COPY",BODY,{"derivedFrom":makeQuery(id+"F8.opPattern","COPY",BODY,{"derivedFrom":makeQuery(id+"F7.opPattern","COPY",BODY,{"derivedFrom":makeQuery(id+"F4.opPattern","COPY",BODY,{"derivedFrom":makeQuery(id+"F2.opPattern","COPY",BODY,{"derivedFrom":makeQuery(id+"F1.opRevolve","SWEPT_BODY",BODY,{"disambiguationData":[OSD([sQuery(id+"F0.wireOp",EDGE,"E1")])]}),"instanceName":"1"}),"instanceName":"1"}),"instanceName":"1"}),"instanceName":"1"}),"instanceName":"1"}),"instanceName":"1"});
            var Q556;
            Q556=makeQuery(id+"F11.opPattern","COPY",BODY,{"derivedFrom":makeQuery(id+"F9.opPattern","COPY",BODY,{"derivedFrom":makeQuery(id+"F8.opPattern","COPY",BODY,{"derivedFrom":makeQuery(id+"F7.opPattern","COPY",BODY,{"derivedFrom":makeQuery(id+"F4.opPattern","COPY",BODY,{"derivedFrom":makeQuery(id+"F3.opPattern","COPY",BODY,{"derivedFrom":makeQuery(id+"F2.opPattern","COPY",BODY,{"derivedFrom":makeQuery(id+"F1.opRevolve","SWEPT_BODY",BODY,{"disambiguationData":[OSD([sQuery(id+"F0.wireOp",EDGE,"E1")])]}),"instanceName":"1"}),"instanceName":"1"}),"instanceName":"1"}),"instanceName":"1"}),"instanceName":"1"}),"instanceName":"1"}),"instanceName":"1"});
            var Q557;
            Q557=makeQuery(id+"F11.opPattern","COPY",BODY,{"derivedFrom":makeQuery(id+"F9.opPattern","COPY",BODY,{"derivedFrom":makeQuery(id+"F8.opPattern","COPY",BODY,{"derivedFrom":makeQuery(id+"F7.opPattern","COPY",BODY,{"derivedFrom":makeQuery(id+"F5.opPattern","COPY",BODY,{"derivedFrom":makeQuery(id+"F1.opRevolve","SWEPT_BODY",BODY,{"disambiguationData":[OSD([sQuery(id+"F0.wireOp",EDGE,"E1")])]}),"instanceName":"1"}),"instanceName":"1"}),"instanceName":"1"}),"instanceName":"1"}),"instanceName":"1"});
            var Q558;
            Q558=makeQuery(id+"F11.opPattern","COPY",BODY,{"derivedFrom":makeQuery(id+"F9.opPattern","COPY",BODY,{"derivedFrom":makeQuery(id+"F8.opPattern","COPY",BODY,{"derivedFrom":makeQuery(id+"F7.opPattern","COPY",BODY,{"derivedFrom":makeQuery(id+"F5.opPattern","COPY",BODY,{"derivedFrom":makeQuery(id+"F2.opPattern","COPY",BODY,{"derivedFrom":makeQuery(id+"F1.opRevolve","SWEPT_BODY",BODY,{"disambiguationData":[OSD([sQuery(id+"F0.wireOp",EDGE,"E1")])]}),"instanceName":"1"}),"instanceName":"1"}),"instanceName":"1"}),"instanceName":"1"}),"instanceName":"1"}),"instanceName":"1"});
            var Q559;
            Q559=makeQuery(id+"F11.opPattern","COPY",BODY,{"derivedFrom":makeQuery(id+"F9.opPattern","COPY",BODY,{"derivedFrom":makeQuery(id+"F8.opPattern","COPY",BODY,{"derivedFrom":makeQuery(id+"F7.opPattern","COPY",BODY,{"derivedFrom":makeQuery(id+"F5.opPattern","COPY",BODY,{"derivedFrom":makeQuery(id+"F3.opPattern","COPY",BODY,{"derivedFrom":makeQuery(id+"F2.opPattern","COPY",BODY,{"derivedFrom":makeQuery(id+"F1.opRevolve","SWEPT_BODY",BODY,{"disambiguationData":[OSD([sQuery(id+"F0.wireOp",EDGE,"E1")])]}),"instanceName":"1"}),"instanceName":"1"}),"instanceName":"1"}),"instanceName":"1"}),"instanceName":"1"}),"instanceName":"1"}),"instanceName":"1"});
            var Q560;
            Q560=makeQuery(id+"F11.opPattern","COPY",BODY,{"derivedFrom":makeQuery(id+"F9.opPattern","COPY",BODY,{"derivedFrom":makeQuery(id+"F8.opPattern","COPY",BODY,{"derivedFrom":makeQuery(id+"F7.opPattern","COPY",BODY,{"derivedFrom":makeQuery(id+"F5.opPattern","COPY",BODY,{"derivedFrom":makeQuery(id+"F4.opPattern","COPY",BODY,{"derivedFrom":makeQuery(id+"F1.opRevolve","SWEPT_BODY",BODY,{"disambiguationData":[OSD([sQuery(id+"F0.wireOp",EDGE,"E1")])]}),"instanceName":"1"}),"instanceName":"1"}),"instanceName":"1"}),"instanceName":"1"}),"instanceName":"1"}),"instanceName":"1"});
            var Q561;
            Q561=makeQuery(id+"F11.opPattern","COPY",BODY,{"derivedFrom":makeQuery(id+"F9.opPattern","COPY",BODY,{"derivedFrom":makeQuery(id+"F8.opPattern","COPY",BODY,{"derivedFrom":makeQuery(id+"F7.opPattern","COPY",BODY,{"derivedFrom":makeQuery(id+"F5.opPattern","COPY",BODY,{"derivedFrom":makeQuery(id+"F4.opPattern","COPY",BODY,{"derivedFrom":makeQuery(id+"F2.opPattern","COPY",BODY,{"derivedFrom":makeQuery(id+"F1.opRevolve","SWEPT_BODY",BODY,{"disambiguationData":[OSD([sQuery(id+"F0.wireOp",EDGE,"E1")])]}),"instanceName":"1"}),"instanceName":"1"}),"instanceName":"1"}),"instanceName":"1"}),"instanceName":"1"}),"instanceName":"1"}),"instanceName":"1"});
            var Q562;
            Q562=makeQuery(id+"F11.opPattern","COPY",BODY,{"derivedFrom":makeQuery(id+"F9.opPattern","COPY",BODY,{"derivedFrom":makeQuery(id+"F8.opPattern","COPY",BODY,{"derivedFrom":makeQuery(id+"F7.opPattern","COPY",BODY,{"derivedFrom":makeQuery(id+"F5.opPattern","COPY",BODY,{"derivedFrom":makeQuery(id+"F4.opPattern","COPY",BODY,{"derivedFrom":makeQuery(id+"F3.opPattern","COPY",BODY,{"derivedFrom":makeQuery(id+"F2.opPattern","COPY",BODY,{"derivedFrom":makeQuery(id+"F1.opRevolve","SWEPT_BODY",BODY,{"disambiguationData":[OSD([sQuery(id+"F0.wireOp",EDGE,"E1")])]}),"instanceName":"1"}),"instanceName":"1"}),"instanceName":"1"}),"instanceName":"1"}),"instanceName":"1"}),"instanceName":"1"}),"instanceName":"1"}),"instanceName":"1"});
            var Q563;
            Q563=makeQuery(id+"F11.opPattern","COPY",BODY,{"derivedFrom":makeQuery(id+"F9.opPattern","COPY",BODY,{"derivedFrom":makeQuery(id+"F8.opPattern","COPY",BODY,{"derivedFrom":makeQuery(id+"F7.opPattern","COPY",BODY,{"derivedFrom":makeQuery(id+"F6.opPattern","COPY",BODY,{"derivedFrom":makeQuery(id+"F1.opRevolve","SWEPT_BODY",BODY,{"disambiguationData":[OSD([sQuery(id+"F0.wireOp",EDGE,"E1")])]}),"instanceName":"1"}),"instanceName":"1"}),"instanceName":"1"}),"instanceName":"1"}),"instanceName":"1"});
            var Q564;
            Q564=makeQuery(id+"F11.opPattern","COPY",BODY,{"derivedFrom":makeQuery(id+"F9.opPattern","COPY",BODY,{"derivedFrom":makeQuery(id+"F8.opPattern","COPY",BODY,{"derivedFrom":makeQuery(id+"F7.opPattern","COPY",BODY,{"derivedFrom":makeQuery(id+"F6.opPattern","COPY",BODY,{"derivedFrom":makeQuery(id+"F2.opPattern","COPY",BODY,{"derivedFrom":makeQuery(id+"F1.opRevolve","SWEPT_BODY",BODY,{"disambiguationData":[OSD([sQuery(id+"F0.wireOp",EDGE,"E1")])]}),"instanceName":"1"}),"instanceName":"1"}),"instanceName":"1"}),"instanceName":"1"}),"instanceName":"1"}),"instanceName":"1"});
            var Q565;
            Q565=makeQuery(id+"F11.opPattern","COPY",BODY,{"derivedFrom":makeQuery(id+"F9.opPattern","COPY",BODY,{"derivedFrom":makeQuery(id+"F8.opPattern","COPY",BODY,{"derivedFrom":makeQuery(id+"F7.opPattern","COPY",BODY,{"derivedFrom":makeQuery(id+"F6.opPattern","COPY",BODY,{"derivedFrom":makeQuery(id+"F3.opPattern","COPY",BODY,{"derivedFrom":makeQuery(id+"F2.opPattern","COPY",BODY,{"derivedFrom":makeQuery(id+"F1.opRevolve","SWEPT_BODY",BODY,{"disambiguationData":[OSD([sQuery(id+"F0.wireOp",EDGE,"E1")])]}),"instanceName":"1"}),"instanceName":"1"}),"instanceName":"1"}),"instanceName":"1"}),"instanceName":"1"}),"instanceName":"1"}),"instanceName":"1"});
            var Q566;
            Q566=makeQuery(id+"F11.opPattern","COPY",BODY,{"derivedFrom":makeQuery(id+"F9.opPattern","COPY",BODY,{"derivedFrom":makeQuery(id+"F8.opPattern","COPY",BODY,{"derivedFrom":makeQuery(id+"F7.opPattern","COPY",BODY,{"derivedFrom":makeQuery(id+"F6.opPattern","COPY",BODY,{"derivedFrom":makeQuery(id+"F4.opPattern","COPY",BODY,{"derivedFrom":makeQuery(id+"F1.opRevolve","SWEPT_BODY",BODY,{"disambiguationData":[OSD([sQuery(id+"F0.wireOp",EDGE,"E1")])]}),"instanceName":"1"}),"instanceName":"1"}),"instanceName":"1"}),"instanceName":"1"}),"instanceName":"1"}),"instanceName":"1"});
            var Q567;
            Q567=makeQuery(id+"F11.opPattern","COPY",BODY,{"derivedFrom":makeQuery(id+"F9.opPattern","COPY",BODY,{"derivedFrom":makeQuery(id+"F8.opPattern","COPY",BODY,{"derivedFrom":makeQuery(id+"F7.opPattern","COPY",BODY,{"derivedFrom":makeQuery(id+"F6.opPattern","COPY",BODY,{"derivedFrom":makeQuery(id+"F4.opPattern","COPY",BODY,{"derivedFrom":makeQuery(id+"F2.opPattern","COPY",BODY,{"derivedFrom":makeQuery(id+"F1.opRevolve","SWEPT_BODY",BODY,{"disambiguationData":[OSD([sQuery(id+"F0.wireOp",EDGE,"E1")])]}),"instanceName":"1"}),"instanceName":"1"}),"instanceName":"1"}),"instanceName":"1"}),"instanceName":"1"}),"instanceName":"1"}),"instanceName":"1"});
            var Q568;
            Q568=makeQuery(id+"F11.opPattern","COPY",BODY,{"derivedFrom":makeQuery(id+"F9.opPattern","COPY",BODY,{"derivedFrom":makeQuery(id+"F8.opPattern","COPY",BODY,{"derivedFrom":makeQuery(id+"F7.opPattern","COPY",BODY,{"derivedFrom":makeQuery(id+"F6.opPattern","COPY",BODY,{"derivedFrom":makeQuery(id+"F4.opPattern","COPY",BODY,{"derivedFrom":makeQuery(id+"F3.opPattern","COPY",BODY,{"derivedFrom":makeQuery(id+"F2.opPattern","COPY",BODY,{"derivedFrom":makeQuery(id+"F1.opRevolve","SWEPT_BODY",BODY,{"disambiguationData":[OSD([sQuery(id+"F0.wireOp",EDGE,"E1")])]}),"instanceName":"1"}),"instanceName":"1"}),"instanceName":"1"}),"instanceName":"1"}),"instanceName":"1"}),"instanceName":"1"}),"instanceName":"1"}),"instanceName":"1"});
            var Q569;
            Q569=makeQuery(id+"F11.opPattern","COPY",BODY,{"derivedFrom":makeQuery(id+"F9.opPattern","COPY",BODY,{"derivedFrom":makeQuery(id+"F8.opPattern","COPY",BODY,{"derivedFrom":makeQuery(id+"F7.opPattern","COPY",BODY,{"derivedFrom":makeQuery(id+"F6.opPattern","COPY",BODY,{"derivedFrom":makeQuery(id+"F5.opPattern","COPY",BODY,{"derivedFrom":makeQuery(id+"F1.opRevolve","SWEPT_BODY",BODY,{"disambiguationData":[OSD([sQuery(id+"F0.wireOp",EDGE,"E1")])]}),"instanceName":"1"}),"instanceName":"1"}),"instanceName":"1"}),"instanceName":"1"}),"instanceName":"1"}),"instanceName":"1"});
            var Q570;
            Q570=makeQuery(id+"F11.opPattern","COPY",BODY,{"derivedFrom":makeQuery(id+"F9.opPattern","COPY",BODY,{"derivedFrom":makeQuery(id+"F8.opPattern","COPY",BODY,{"derivedFrom":makeQuery(id+"F7.opPattern","COPY",BODY,{"derivedFrom":makeQuery(id+"F6.opPattern","COPY",BODY,{"derivedFrom":makeQuery(id+"F5.opPattern","COPY",BODY,{"derivedFrom":makeQuery(id+"F2.opPattern","COPY",BODY,{"derivedFrom":makeQuery(id+"F1.opRevolve","SWEPT_BODY",BODY,{"disambiguationData":[OSD([sQuery(id+"F0.wireOp",EDGE,"E1")])]}),"instanceName":"1"}),"instanceName":"1"}),"instanceName":"1"}),"instanceName":"1"}),"instanceName":"1"}),"instanceName":"1"}),"instanceName":"1"});
            var Q571;
            Q571=makeQuery(id+"F11.opPattern","COPY",BODY,{"derivedFrom":makeQuery(id+"F9.opPattern","COPY",BODY,{"derivedFrom":makeQuery(id+"F8.opPattern","COPY",BODY,{"derivedFrom":makeQuery(id+"F7.opPattern","COPY",BODY,{"derivedFrom":makeQuery(id+"F6.opPattern","COPY",BODY,{"derivedFrom":makeQuery(id+"F5.opPattern","COPY",BODY,{"derivedFrom":makeQuery(id+"F3.opPattern","COPY",BODY,{"derivedFrom":makeQuery(id+"F2.opPattern","COPY",BODY,{"derivedFrom":makeQuery(id+"F1.opRevolve","SWEPT_BODY",BODY,{"disambiguationData":[OSD([sQuery(id+"F0.wireOp",EDGE,"E1")])]}),"instanceName":"1"}),"instanceName":"1"}),"instanceName":"1"}),"instanceName":"1"}),"instanceName":"1"}),"instanceName":"1"}),"instanceName":"1"}),"instanceName":"1"});
            var Q572;
            Q572=makeQuery(id+"F11.opPattern","COPY",BODY,{"derivedFrom":makeQuery(id+"F9.opPattern","COPY",BODY,{"derivedFrom":makeQuery(id+"F8.opPattern","COPY",BODY,{"derivedFrom":makeQuery(id+"F7.opPattern","COPY",BODY,{"derivedFrom":makeQuery(id+"F6.opPattern","COPY",BODY,{"derivedFrom":makeQuery(id+"F5.opPattern","COPY",BODY,{"derivedFrom":makeQuery(id+"F4.opPattern","COPY",BODY,{"derivedFrom":makeQuery(id+"F1.opRevolve","SWEPT_BODY",BODY,{"disambiguationData":[OSD([sQuery(id+"F0.wireOp",EDGE,"E1")])]}),"instanceName":"1"}),"instanceName":"1"}),"instanceName":"1"}),"instanceName":"1"}),"instanceName":"1"}),"instanceName":"1"}),"instanceName":"1"});
            var Q573;
            Q573=makeQuery(id+"F11.opPattern","COPY",BODY,{"derivedFrom":makeQuery(id+"F9.opPattern","COPY",BODY,{"derivedFrom":makeQuery(id+"F8.opPattern","COPY",BODY,{"derivedFrom":makeQuery(id+"F7.opPattern","COPY",BODY,{"derivedFrom":makeQuery(id+"F6.opPattern","COPY",BODY,{"derivedFrom":makeQuery(id+"F5.opPattern","COPY",BODY,{"derivedFrom":makeQuery(id+"F4.opPattern","COPY",BODY,{"derivedFrom":makeQuery(id+"F2.opPattern","COPY",BODY,{"derivedFrom":makeQuery(id+"F1.opRevolve","SWEPT_BODY",BODY,{"disambiguationData":[OSD([sQuery(id+"F0.wireOp",EDGE,"E1")])]}),"instanceName":"1"}),"instanceName":"1"}),"instanceName":"1"}),"instanceName":"1"}),"instanceName":"1"}),"instanceName":"1"}),"instanceName":"1"}),"instanceName":"1"});
            var Q574;
            Q574=makeQuery(id+"F11.opPattern","COPY",BODY,{"derivedFrom":makeQuery(id+"F9.opPattern","COPY",BODY,{"derivedFrom":makeQuery(id+"F8.opPattern","COPY",BODY,{"derivedFrom":makeQuery(id+"F7.opPattern","COPY",BODY,{"derivedFrom":makeQuery(id+"F6.opPattern","COPY",BODY,{"derivedFrom":makeQuery(id+"F5.opPattern","COPY",BODY,{"derivedFrom":makeQuery(id+"F4.opPattern","COPY",BODY,{"derivedFrom":makeQuery(id+"F3.opPattern","COPY",BODY,{"derivedFrom":makeQuery(id+"F2.opPattern","COPY",BODY,{"derivedFrom":makeQuery(id+"F1.opRevolve","SWEPT_BODY",BODY,{"disambiguationData":[OSD([sQuery(id+"F0.wireOp",EDGE,"E1")])]}),"instanceName":"1"}),"instanceName":"1"}),"instanceName":"1"}),"instanceName":"1"}),"instanceName":"1"}),"instanceName":"1"}),"instanceName":"1"}),"instanceName":"1"}),"instanceName":"1"});
            var Q575;
            Q575=makeQuery(id+"F11.opPattern","COPY",BODY,{"derivedFrom":makeQuery(id+"F10.opPattern","COPY",BODY,{"derivedFrom":makeQuery(id+"F1.opRevolve","SWEPT_BODY",BODY,{"disambiguationData":[OSD([sQuery(id+"F0.wireOp",EDGE,"E1")])]}),"instanceName":"1"}),"instanceName":"1"});
            var Q576;
            Q576=makeQuery(id+"F11.opPattern","COPY",BODY,{"derivedFrom":makeQuery(id+"F10.opPattern","COPY",BODY,{"derivedFrom":makeQuery(id+"F2.opPattern","COPY",BODY,{"derivedFrom":makeQuery(id+"F1.opRevolve","SWEPT_BODY",BODY,{"disambiguationData":[OSD([sQuery(id+"F0.wireOp",EDGE,"E1")])]}),"instanceName":"1"}),"instanceName":"1"}),"instanceName":"1"});
            var Q577;
            Q577=makeQuery(id+"F11.opPattern","COPY",BODY,{"derivedFrom":makeQuery(id+"F10.opPattern","COPY",BODY,{"derivedFrom":makeQuery(id+"F3.opPattern","COPY",BODY,{"derivedFrom":makeQuery(id+"F2.opPattern","COPY",BODY,{"derivedFrom":makeQuery(id+"F1.opRevolve","SWEPT_BODY",BODY,{"disambiguationData":[OSD([sQuery(id+"F0.wireOp",EDGE,"E1")])]}),"instanceName":"1"}),"instanceName":"1"}),"instanceName":"1"}),"instanceName":"1"});
            var Q578;
            Q578=makeQuery(id+"F11.opPattern","COPY",BODY,{"derivedFrom":makeQuery(id+"F10.opPattern","COPY",BODY,{"derivedFrom":makeQuery(id+"F4.opPattern","COPY",BODY,{"derivedFrom":makeQuery(id+"F1.opRevolve","SWEPT_BODY",BODY,{"disambiguationData":[OSD([sQuery(id+"F0.wireOp",EDGE,"E1")])]}),"instanceName":"1"}),"instanceName":"1"}),"instanceName":"1"});
            var Q579;
            Q579=makeQuery(id+"F11.opPattern","COPY",BODY,{"derivedFrom":makeQuery(id+"F10.opPattern","COPY",BODY,{"derivedFrom":makeQuery(id+"F4.opPattern","COPY",BODY,{"derivedFrom":makeQuery(id+"F2.opPattern","COPY",BODY,{"derivedFrom":makeQuery(id+"F1.opRevolve","SWEPT_BODY",BODY,{"disambiguationData":[OSD([sQuery(id+"F0.wireOp",EDGE,"E1")])]}),"instanceName":"1"}),"instanceName":"1"}),"instanceName":"1"}),"instanceName":"1"});
            var Q580;
            Q580=makeQuery(id+"F11.opPattern","COPY",BODY,{"derivedFrom":makeQuery(id+"F10.opPattern","COPY",BODY,{"derivedFrom":makeQuery(id+"F4.opPattern","COPY",BODY,{"derivedFrom":makeQuery(id+"F3.opPattern","COPY",BODY,{"derivedFrom":makeQuery(id+"F2.opPattern","COPY",BODY,{"derivedFrom":makeQuery(id+"F1.opRevolve","SWEPT_BODY",BODY,{"disambiguationData":[OSD([sQuery(id+"F0.wireOp",EDGE,"E1")])]}),"instanceName":"1"}),"instanceName":"1"}),"instanceName":"1"}),"instanceName":"1"}),"instanceName":"1"});
            var Q581;
            Q581=makeQuery(id+"F11.opPattern","COPY",BODY,{"derivedFrom":makeQuery(id+"F10.opPattern","COPY",BODY,{"derivedFrom":makeQuery(id+"F5.opPattern","COPY",BODY,{"derivedFrom":makeQuery(id+"F1.opRevolve","SWEPT_BODY",BODY,{"disambiguationData":[OSD([sQuery(id+"F0.wireOp",EDGE,"E1")])]}),"instanceName":"1"}),"instanceName":"1"}),"instanceName":"1"});
            var Q582;
            Q582=makeQuery(id+"F11.opPattern","COPY",BODY,{"derivedFrom":makeQuery(id+"F10.opPattern","COPY",BODY,{"derivedFrom":makeQuery(id+"F5.opPattern","COPY",BODY,{"derivedFrom":makeQuery(id+"F2.opPattern","COPY",BODY,{"derivedFrom":makeQuery(id+"F1.opRevolve","SWEPT_BODY",BODY,{"disambiguationData":[OSD([sQuery(id+"F0.wireOp",EDGE,"E1")])]}),"instanceName":"1"}),"instanceName":"1"}),"instanceName":"1"}),"instanceName":"1"});
            var Q583;
            Q583=makeQuery(id+"F11.opPattern","COPY",BODY,{"derivedFrom":makeQuery(id+"F10.opPattern","COPY",BODY,{"derivedFrom":makeQuery(id+"F5.opPattern","COPY",BODY,{"derivedFrom":makeQuery(id+"F3.opPattern","COPY",BODY,{"derivedFrom":makeQuery(id+"F2.opPattern","COPY",BODY,{"derivedFrom":makeQuery(id+"F1.opRevolve","SWEPT_BODY",BODY,{"disambiguationData":[OSD([sQuery(id+"F0.wireOp",EDGE,"E1")])]}),"instanceName":"1"}),"instanceName":"1"}),"instanceName":"1"}),"instanceName":"1"}),"instanceName":"1"});
            var Q584;
            Q584=makeQuery(id+"F11.opPattern","COPY",BODY,{"derivedFrom":makeQuery(id+"F10.opPattern","COPY",BODY,{"derivedFrom":makeQuery(id+"F5.opPattern","COPY",BODY,{"derivedFrom":makeQuery(id+"F4.opPattern","COPY",BODY,{"derivedFrom":makeQuery(id+"F1.opRevolve","SWEPT_BODY",BODY,{"disambiguationData":[OSD([sQuery(id+"F0.wireOp",EDGE,"E1")])]}),"instanceName":"1"}),"instanceName":"1"}),"instanceName":"1"}),"instanceName":"1"});
            var Q585;
            Q585=makeQuery(id+"F11.opPattern","COPY",BODY,{"derivedFrom":makeQuery(id+"F10.opPattern","COPY",BODY,{"derivedFrom":makeQuery(id+"F5.opPattern","COPY",BODY,{"derivedFrom":makeQuery(id+"F4.opPattern","COPY",BODY,{"derivedFrom":makeQuery(id+"F2.opPattern","COPY",BODY,{"derivedFrom":makeQuery(id+"F1.opRevolve","SWEPT_BODY",BODY,{"disambiguationData":[OSD([sQuery(id+"F0.wireOp",EDGE,"E1")])]}),"instanceName":"1"}),"instanceName":"1"}),"instanceName":"1"}),"instanceName":"1"}),"instanceName":"1"});
            var Q586;
            Q586=makeQuery(id+"F11.opPattern","COPY",BODY,{"derivedFrom":makeQuery(id+"F10.opPattern","COPY",BODY,{"derivedFrom":makeQuery(id+"F5.opPattern","COPY",BODY,{"derivedFrom":makeQuery(id+"F4.opPattern","COPY",BODY,{"derivedFrom":makeQuery(id+"F3.opPattern","COPY",BODY,{"derivedFrom":makeQuery(id+"F2.opPattern","COPY",BODY,{"derivedFrom":makeQuery(id+"F1.opRevolve","SWEPT_BODY",BODY,{"disambiguationData":[OSD([sQuery(id+"F0.wireOp",EDGE,"E1")])]}),"instanceName":"1"}),"instanceName":"1"}),"instanceName":"1"}),"instanceName":"1"}),"instanceName":"1"}),"instanceName":"1"});
            var Q587;
            Q587=makeQuery(id+"F11.opPattern","COPY",BODY,{"derivedFrom":makeQuery(id+"F10.opPattern","COPY",BODY,{"derivedFrom":makeQuery(id+"F6.opPattern","COPY",BODY,{"derivedFrom":makeQuery(id+"F1.opRevolve","SWEPT_BODY",BODY,{"disambiguationData":[OSD([sQuery(id+"F0.wireOp",EDGE,"E1")])]}),"instanceName":"1"}),"instanceName":"1"}),"instanceName":"1"});
            var Q588;
            Q588=makeQuery(id+"F11.opPattern","COPY",BODY,{"derivedFrom":makeQuery(id+"F10.opPattern","COPY",BODY,{"derivedFrom":makeQuery(id+"F6.opPattern","COPY",BODY,{"derivedFrom":makeQuery(id+"F2.opPattern","COPY",BODY,{"derivedFrom":makeQuery(id+"F1.opRevolve","SWEPT_BODY",BODY,{"disambiguationData":[OSD([sQuery(id+"F0.wireOp",EDGE,"E1")])]}),"instanceName":"1"}),"instanceName":"1"}),"instanceName":"1"}),"instanceName":"1"});
            var Q589;
            Q589=makeQuery(id+"F11.opPattern","COPY",BODY,{"derivedFrom":makeQuery(id+"F10.opPattern","COPY",BODY,{"derivedFrom":makeQuery(id+"F6.opPattern","COPY",BODY,{"derivedFrom":makeQuery(id+"F3.opPattern","COPY",BODY,{"derivedFrom":makeQuery(id+"F2.opPattern","COPY",BODY,{"derivedFrom":makeQuery(id+"F1.opRevolve","SWEPT_BODY",BODY,{"disambiguationData":[OSD([sQuery(id+"F0.wireOp",EDGE,"E1")])]}),"instanceName":"1"}),"instanceName":"1"}),"instanceName":"1"}),"instanceName":"1"}),"instanceName":"1"});
            var Q590;
            Q590=makeQuery(id+"F11.opPattern","COPY",BODY,{"derivedFrom":makeQuery(id+"F10.opPattern","COPY",BODY,{"derivedFrom":makeQuery(id+"F6.opPattern","COPY",BODY,{"derivedFrom":makeQuery(id+"F4.opPattern","COPY",BODY,{"derivedFrom":makeQuery(id+"F1.opRevolve","SWEPT_BODY",BODY,{"disambiguationData":[OSD([sQuery(id+"F0.wireOp",EDGE,"E1")])]}),"instanceName":"1"}),"instanceName":"1"}),"instanceName":"1"}),"instanceName":"1"});
            var Q591;
            Q591=makeQuery(id+"F11.opPattern","COPY",BODY,{"derivedFrom":makeQuery(id+"F10.opPattern","COPY",BODY,{"derivedFrom":makeQuery(id+"F6.opPattern","COPY",BODY,{"derivedFrom":makeQuery(id+"F4.opPattern","COPY",BODY,{"derivedFrom":makeQuery(id+"F2.opPattern","COPY",BODY,{"derivedFrom":makeQuery(id+"F1.opRevolve","SWEPT_BODY",BODY,{"disambiguationData":[OSD([sQuery(id+"F0.wireOp",EDGE,"E1")])]}),"instanceName":"1"}),"instanceName":"1"}),"instanceName":"1"}),"instanceName":"1"}),"instanceName":"1"});
            var Q592;
            Q592=makeQuery(id+"F11.opPattern","COPY",BODY,{"derivedFrom":makeQuery(id+"F10.opPattern","COPY",BODY,{"derivedFrom":makeQuery(id+"F6.opPattern","COPY",BODY,{"derivedFrom":makeQuery(id+"F4.opPattern","COPY",BODY,{"derivedFrom":makeQuery(id+"F3.opPattern","COPY",BODY,{"derivedFrom":makeQuery(id+"F2.opPattern","COPY",BODY,{"derivedFrom":makeQuery(id+"F1.opRevolve","SWEPT_BODY",BODY,{"disambiguationData":[OSD([sQuery(id+"F0.wireOp",EDGE,"E1")])]}),"instanceName":"1"}),"instanceName":"1"}),"instanceName":"1"}),"instanceName":"1"}),"instanceName":"1"}),"instanceName":"1"});
            var Q593;
            Q593=makeQuery(id+"F11.opPattern","COPY",BODY,{"derivedFrom":makeQuery(id+"F10.opPattern","COPY",BODY,{"derivedFrom":makeQuery(id+"F6.opPattern","COPY",BODY,{"derivedFrom":makeQuery(id+"F5.opPattern","COPY",BODY,{"derivedFrom":makeQuery(id+"F1.opRevolve","SWEPT_BODY",BODY,{"disambiguationData":[OSD([sQuery(id+"F0.wireOp",EDGE,"E1")])]}),"instanceName":"1"}),"instanceName":"1"}),"instanceName":"1"}),"instanceName":"1"});
            var Q594;
            Q594=makeQuery(id+"F11.opPattern","COPY",BODY,{"derivedFrom":makeQuery(id+"F10.opPattern","COPY",BODY,{"derivedFrom":makeQuery(id+"F6.opPattern","COPY",BODY,{"derivedFrom":makeQuery(id+"F5.opPattern","COPY",BODY,{"derivedFrom":makeQuery(id+"F2.opPattern","COPY",BODY,{"derivedFrom":makeQuery(id+"F1.opRevolve","SWEPT_BODY",BODY,{"disambiguationData":[OSD([sQuery(id+"F0.wireOp",EDGE,"E1")])]}),"instanceName":"1"}),"instanceName":"1"}),"instanceName":"1"}),"instanceName":"1"}),"instanceName":"1"});
            var Q595;
            Q595=makeQuery(id+"F11.opPattern","COPY",BODY,{"derivedFrom":makeQuery(id+"F10.opPattern","COPY",BODY,{"derivedFrom":makeQuery(id+"F6.opPattern","COPY",BODY,{"derivedFrom":makeQuery(id+"F5.opPattern","COPY",BODY,{"derivedFrom":makeQuery(id+"F3.opPattern","COPY",BODY,{"derivedFrom":makeQuery(id+"F2.opPattern","COPY",BODY,{"derivedFrom":makeQuery(id+"F1.opRevolve","SWEPT_BODY",BODY,{"disambiguationData":[OSD([sQuery(id+"F0.wireOp",EDGE,"E1")])]}),"instanceName":"1"}),"instanceName":"1"}),"instanceName":"1"}),"instanceName":"1"}),"instanceName":"1"}),"instanceName":"1"});
            var Q596;
            Q596=makeQuery(id+"F11.opPattern","COPY",BODY,{"derivedFrom":makeQuery(id+"F10.opPattern","COPY",BODY,{"derivedFrom":makeQuery(id+"F6.opPattern","COPY",BODY,{"derivedFrom":makeQuery(id+"F5.opPattern","COPY",BODY,{"derivedFrom":makeQuery(id+"F4.opPattern","COPY",BODY,{"derivedFrom":makeQuery(id+"F1.opRevolve","SWEPT_BODY",BODY,{"disambiguationData":[OSD([sQuery(id+"F0.wireOp",EDGE,"E1")])]}),"instanceName":"1"}),"instanceName":"1"}),"instanceName":"1"}),"instanceName":"1"}),"instanceName":"1"});
            var Q597;
            Q597=makeQuery(id+"F11.opPattern","COPY",BODY,{"derivedFrom":makeQuery(id+"F10.opPattern","COPY",BODY,{"derivedFrom":makeQuery(id+"F6.opPattern","COPY",BODY,{"derivedFrom":makeQuery(id+"F5.opPattern","COPY",BODY,{"derivedFrom":makeQuery(id+"F4.opPattern","COPY",BODY,{"derivedFrom":makeQuery(id+"F2.opPattern","COPY",BODY,{"derivedFrom":makeQuery(id+"F1.opRevolve","SWEPT_BODY",BODY,{"disambiguationData":[OSD([sQuery(id+"F0.wireOp",EDGE,"E1")])]}),"instanceName":"1"}),"instanceName":"1"}),"instanceName":"1"}),"instanceName":"1"}),"instanceName":"1"}),"instanceName":"1"});
            var Q598;
            Q598=makeQuery(id+"F11.opPattern","COPY",BODY,{"derivedFrom":makeQuery(id+"F10.opPattern","COPY",BODY,{"derivedFrom":makeQuery(id+"F6.opPattern","COPY",BODY,{"derivedFrom":makeQuery(id+"F5.opPattern","COPY",BODY,{"derivedFrom":makeQuery(id+"F4.opPattern","COPY",BODY,{"derivedFrom":makeQuery(id+"F3.opPattern","COPY",BODY,{"derivedFrom":makeQuery(id+"F2.opPattern","COPY",BODY,{"derivedFrom":makeQuery(id+"F1.opRevolve","SWEPT_BODY",BODY,{"disambiguationData":[OSD([sQuery(id+"F0.wireOp",EDGE,"E1")])]}),"instanceName":"1"}),"instanceName":"1"}),"instanceName":"1"}),"instanceName":"1"}),"instanceName":"1"}),"instanceName":"1"}),"instanceName":"1"});
            var Q599;
            Q599=makeQuery(id+"F11.opPattern","COPY",BODY,{"derivedFrom":makeQuery(id+"F10.opPattern","COPY",BODY,{"derivedFrom":makeQuery(id+"F7.opPattern","COPY",BODY,{"derivedFrom":makeQuery(id+"F1.opRevolve","SWEPT_BODY",BODY,{"disambiguationData":[OSD([sQuery(id+"F0.wireOp",EDGE,"E1")])]}),"instanceName":"1"}),"instanceName":"1"}),"instanceName":"1"});
            var Q600;
            Q600=makeQuery(id+"F11.opPattern","COPY",BODY,{"derivedFrom":makeQuery(id+"F10.opPattern","COPY",BODY,{"derivedFrom":makeQuery(id+"F7.opPattern","COPY",BODY,{"derivedFrom":makeQuery(id+"F2.opPattern","COPY",BODY,{"derivedFrom":makeQuery(id+"F1.opRevolve","SWEPT_BODY",BODY,{"disambiguationData":[OSD([sQuery(id+"F0.wireOp",EDGE,"E1")])]}),"instanceName":"1"}),"instanceName":"1"}),"instanceName":"1"}),"instanceName":"1"});
            var Q601;
            Q601=makeQuery(id+"F11.opPattern","COPY",BODY,{"derivedFrom":makeQuery(id+"F10.opPattern","COPY",BODY,{"derivedFrom":makeQuery(id+"F7.opPattern","COPY",BODY,{"derivedFrom":makeQuery(id+"F3.opPattern","COPY",BODY,{"derivedFrom":makeQuery(id+"F2.opPattern","COPY",BODY,{"derivedFrom":makeQuery(id+"F1.opRevolve","SWEPT_BODY",BODY,{"disambiguationData":[OSD([sQuery(id+"F0.wireOp",EDGE,"E1")])]}),"instanceName":"1"}),"instanceName":"1"}),"instanceName":"1"}),"instanceName":"1"}),"instanceName":"1"});
            var Q602;
            Q602=makeQuery(id+"F11.opPattern","COPY",BODY,{"derivedFrom":makeQuery(id+"F10.opPattern","COPY",BODY,{"derivedFrom":makeQuery(id+"F7.opPattern","COPY",BODY,{"derivedFrom":makeQuery(id+"F4.opPattern","COPY",BODY,{"derivedFrom":makeQuery(id+"F1.opRevolve","SWEPT_BODY",BODY,{"disambiguationData":[OSD([sQuery(id+"F0.wireOp",EDGE,"E1")])]}),"instanceName":"1"}),"instanceName":"1"}),"instanceName":"1"}),"instanceName":"1"});
            var Q603;
            Q603=makeQuery(id+"F11.opPattern","COPY",BODY,{"derivedFrom":makeQuery(id+"F10.opPattern","COPY",BODY,{"derivedFrom":makeQuery(id+"F7.opPattern","COPY",BODY,{"derivedFrom":makeQuery(id+"F4.opPattern","COPY",BODY,{"derivedFrom":makeQuery(id+"F2.opPattern","COPY",BODY,{"derivedFrom":makeQuery(id+"F1.opRevolve","SWEPT_BODY",BODY,{"disambiguationData":[OSD([sQuery(id+"F0.wireOp",EDGE,"E1")])]}),"instanceName":"1"}),"instanceName":"1"}),"instanceName":"1"}),"instanceName":"1"}),"instanceName":"1"});
            var Q604;
            Q604=makeQuery(id+"F11.opPattern","COPY",BODY,{"derivedFrom":makeQuery(id+"F10.opPattern","COPY",BODY,{"derivedFrom":makeQuery(id+"F7.opPattern","COPY",BODY,{"derivedFrom":makeQuery(id+"F4.opPattern","COPY",BODY,{"derivedFrom":makeQuery(id+"F3.opPattern","COPY",BODY,{"derivedFrom":makeQuery(id+"F2.opPattern","COPY",BODY,{"derivedFrom":makeQuery(id+"F1.opRevolve","SWEPT_BODY",BODY,{"disambiguationData":[OSD([sQuery(id+"F0.wireOp",EDGE,"E1")])]}),"instanceName":"1"}),"instanceName":"1"}),"instanceName":"1"}),"instanceName":"1"}),"instanceName":"1"}),"instanceName":"1"});
            var Q605;
            Q605=makeQuery(id+"F11.opPattern","COPY",BODY,{"derivedFrom":makeQuery(id+"F10.opPattern","COPY",BODY,{"derivedFrom":makeQuery(id+"F7.opPattern","COPY",BODY,{"derivedFrom":makeQuery(id+"F5.opPattern","COPY",BODY,{"derivedFrom":makeQuery(id+"F1.opRevolve","SWEPT_BODY",BODY,{"disambiguationData":[OSD([sQuery(id+"F0.wireOp",EDGE,"E1")])]}),"instanceName":"1"}),"instanceName":"1"}),"instanceName":"1"}),"instanceName":"1"});
            var Q606;
            Q606=makeQuery(id+"F11.opPattern","COPY",BODY,{"derivedFrom":makeQuery(id+"F10.opPattern","COPY",BODY,{"derivedFrom":makeQuery(id+"F7.opPattern","COPY",BODY,{"derivedFrom":makeQuery(id+"F5.opPattern","COPY",BODY,{"derivedFrom":makeQuery(id+"F2.opPattern","COPY",BODY,{"derivedFrom":makeQuery(id+"F1.opRevolve","SWEPT_BODY",BODY,{"disambiguationData":[OSD([sQuery(id+"F0.wireOp",EDGE,"E1")])]}),"instanceName":"1"}),"instanceName":"1"}),"instanceName":"1"}),"instanceName":"1"}),"instanceName":"1"});
            var Q607;
            Q607=makeQuery(id+"F11.opPattern","COPY",BODY,{"derivedFrom":makeQuery(id+"F10.opPattern","COPY",BODY,{"derivedFrom":makeQuery(id+"F7.opPattern","COPY",BODY,{"derivedFrom":makeQuery(id+"F5.opPattern","COPY",BODY,{"derivedFrom":makeQuery(id+"F3.opPattern","COPY",BODY,{"derivedFrom":makeQuery(id+"F2.opPattern","COPY",BODY,{"derivedFrom":makeQuery(id+"F1.opRevolve","SWEPT_BODY",BODY,{"disambiguationData":[OSD([sQuery(id+"F0.wireOp",EDGE,"E1")])]}),"instanceName":"1"}),"instanceName":"1"}),"instanceName":"1"}),"instanceName":"1"}),"instanceName":"1"}),"instanceName":"1"});
            var Q608;
            Q608=makeQuery(id+"F11.opPattern","COPY",BODY,{"derivedFrom":makeQuery(id+"F10.opPattern","COPY",BODY,{"derivedFrom":makeQuery(id+"F7.opPattern","COPY",BODY,{"derivedFrom":makeQuery(id+"F5.opPattern","COPY",BODY,{"derivedFrom":makeQuery(id+"F4.opPattern","COPY",BODY,{"derivedFrom":makeQuery(id+"F1.opRevolve","SWEPT_BODY",BODY,{"disambiguationData":[OSD([sQuery(id+"F0.wireOp",EDGE,"E1")])]}),"instanceName":"1"}),"instanceName":"1"}),"instanceName":"1"}),"instanceName":"1"}),"instanceName":"1"});
            var Q609;
            Q609=makeQuery(id+"F11.opPattern","COPY",BODY,{"derivedFrom":makeQuery(id+"F10.opPattern","COPY",BODY,{"derivedFrom":makeQuery(id+"F7.opPattern","COPY",BODY,{"derivedFrom":makeQuery(id+"F5.opPattern","COPY",BODY,{"derivedFrom":makeQuery(id+"F4.opPattern","COPY",BODY,{"derivedFrom":makeQuery(id+"F2.opPattern","COPY",BODY,{"derivedFrom":makeQuery(id+"F1.opRevolve","SWEPT_BODY",BODY,{"disambiguationData":[OSD([sQuery(id+"F0.wireOp",EDGE,"E1")])]}),"instanceName":"1"}),"instanceName":"1"}),"instanceName":"1"}),"instanceName":"1"}),"instanceName":"1"}),"instanceName":"1"});
            var Q610;
            Q610=makeQuery(id+"F11.opPattern","COPY",BODY,{"derivedFrom":makeQuery(id+"F10.opPattern","COPY",BODY,{"derivedFrom":makeQuery(id+"F7.opPattern","COPY",BODY,{"derivedFrom":makeQuery(id+"F5.opPattern","COPY",BODY,{"derivedFrom":makeQuery(id+"F4.opPattern","COPY",BODY,{"derivedFrom":makeQuery(id+"F3.opPattern","COPY",BODY,{"derivedFrom":makeQuery(id+"F2.opPattern","COPY",BODY,{"derivedFrom":makeQuery(id+"F1.opRevolve","SWEPT_BODY",BODY,{"disambiguationData":[OSD([sQuery(id+"F0.wireOp",EDGE,"E1")])]}),"instanceName":"1"}),"instanceName":"1"}),"instanceName":"1"}),"instanceName":"1"}),"instanceName":"1"}),"instanceName":"1"}),"instanceName":"1"});
            var Q611;
            Q611=makeQuery(id+"F11.opPattern","COPY",BODY,{"derivedFrom":makeQuery(id+"F10.opPattern","COPY",BODY,{"derivedFrom":makeQuery(id+"F7.opPattern","COPY",BODY,{"derivedFrom":makeQuery(id+"F6.opPattern","COPY",BODY,{"derivedFrom":makeQuery(id+"F1.opRevolve","SWEPT_BODY",BODY,{"disambiguationData":[OSD([sQuery(id+"F0.wireOp",EDGE,"E1")])]}),"instanceName":"1"}),"instanceName":"1"}),"instanceName":"1"}),"instanceName":"1"});
            var Q612;
            Q612=makeQuery(id+"F11.opPattern","COPY",BODY,{"derivedFrom":makeQuery(id+"F10.opPattern","COPY",BODY,{"derivedFrom":makeQuery(id+"F7.opPattern","COPY",BODY,{"derivedFrom":makeQuery(id+"F6.opPattern","COPY",BODY,{"derivedFrom":makeQuery(id+"F2.opPattern","COPY",BODY,{"derivedFrom":makeQuery(id+"F1.opRevolve","SWEPT_BODY",BODY,{"disambiguationData":[OSD([sQuery(id+"F0.wireOp",EDGE,"E1")])]}),"instanceName":"1"}),"instanceName":"1"}),"instanceName":"1"}),"instanceName":"1"}),"instanceName":"1"});
            var Q613;
            Q613=makeQuery(id+"F11.opPattern","COPY",BODY,{"derivedFrom":makeQuery(id+"F10.opPattern","COPY",BODY,{"derivedFrom":makeQuery(id+"F7.opPattern","COPY",BODY,{"derivedFrom":makeQuery(id+"F6.opPattern","COPY",BODY,{"derivedFrom":makeQuery(id+"F3.opPattern","COPY",BODY,{"derivedFrom":makeQuery(id+"F2.opPattern","COPY",BODY,{"derivedFrom":makeQuery(id+"F1.opRevolve","SWEPT_BODY",BODY,{"disambiguationData":[OSD([sQuery(id+"F0.wireOp",EDGE,"E1")])]}),"instanceName":"1"}),"instanceName":"1"}),"instanceName":"1"}),"instanceName":"1"}),"instanceName":"1"}),"instanceName":"1"});
            var Q614;
            Q614=makeQuery(id+"F11.opPattern","COPY",BODY,{"derivedFrom":makeQuery(id+"F10.opPattern","COPY",BODY,{"derivedFrom":makeQuery(id+"F7.opPattern","COPY",BODY,{"derivedFrom":makeQuery(id+"F6.opPattern","COPY",BODY,{"derivedFrom":makeQuery(id+"F4.opPattern","COPY",BODY,{"derivedFrom":makeQuery(id+"F1.opRevolve","SWEPT_BODY",BODY,{"disambiguationData":[OSD([sQuery(id+"F0.wireOp",EDGE,"E1")])]}),"instanceName":"1"}),"instanceName":"1"}),"instanceName":"1"}),"instanceName":"1"}),"instanceName":"1"});
            var Q615;
            Q615=makeQuery(id+"F11.opPattern","COPY",BODY,{"derivedFrom":makeQuery(id+"F10.opPattern","COPY",BODY,{"derivedFrom":makeQuery(id+"F7.opPattern","COPY",BODY,{"derivedFrom":makeQuery(id+"F6.opPattern","COPY",BODY,{"derivedFrom":makeQuery(id+"F4.opPattern","COPY",BODY,{"derivedFrom":makeQuery(id+"F2.opPattern","COPY",BODY,{"derivedFrom":makeQuery(id+"F1.opRevolve","SWEPT_BODY",BODY,{"disambiguationData":[OSD([sQuery(id+"F0.wireOp",EDGE,"E1")])]}),"instanceName":"1"}),"instanceName":"1"}),"instanceName":"1"}),"instanceName":"1"}),"instanceName":"1"}),"instanceName":"1"});
            var Q616;
            Q616=makeQuery(id+"F11.opPattern","COPY",BODY,{"derivedFrom":makeQuery(id+"F10.opPattern","COPY",BODY,{"derivedFrom":makeQuery(id+"F7.opPattern","COPY",BODY,{"derivedFrom":makeQuery(id+"F6.opPattern","COPY",BODY,{"derivedFrom":makeQuery(id+"F4.opPattern","COPY",BODY,{"derivedFrom":makeQuery(id+"F3.opPattern","COPY",BODY,{"derivedFrom":makeQuery(id+"F2.opPattern","COPY",BODY,{"derivedFrom":makeQuery(id+"F1.opRevolve","SWEPT_BODY",BODY,{"disambiguationData":[OSD([sQuery(id+"F0.wireOp",EDGE,"E1")])]}),"instanceName":"1"}),"instanceName":"1"}),"instanceName":"1"}),"instanceName":"1"}),"instanceName":"1"}),"instanceName":"1"}),"instanceName":"1"});
            var Q617;
            Q617=makeQuery(id+"F11.opPattern","COPY",BODY,{"derivedFrom":makeQuery(id+"F10.opPattern","COPY",BODY,{"derivedFrom":makeQuery(id+"F7.opPattern","COPY",BODY,{"derivedFrom":makeQuery(id+"F6.opPattern","COPY",BODY,{"derivedFrom":makeQuery(id+"F5.opPattern","COPY",BODY,{"derivedFrom":makeQuery(id+"F1.opRevolve","SWEPT_BODY",BODY,{"disambiguationData":[OSD([sQuery(id+"F0.wireOp",EDGE,"E1")])]}),"instanceName":"1"}),"instanceName":"1"}),"instanceName":"1"}),"instanceName":"1"}),"instanceName":"1"});
            var Q618;
            Q618=makeQuery(id+"F11.opPattern","COPY",BODY,{"derivedFrom":makeQuery(id+"F10.opPattern","COPY",BODY,{"derivedFrom":makeQuery(id+"F7.opPattern","COPY",BODY,{"derivedFrom":makeQuery(id+"F6.opPattern","COPY",BODY,{"derivedFrom":makeQuery(id+"F5.opPattern","COPY",BODY,{"derivedFrom":makeQuery(id+"F2.opPattern","COPY",BODY,{"derivedFrom":makeQuery(id+"F1.opRevolve","SWEPT_BODY",BODY,{"disambiguationData":[OSD([sQuery(id+"F0.wireOp",EDGE,"E1")])]}),"instanceName":"1"}),"instanceName":"1"}),"instanceName":"1"}),"instanceName":"1"}),"instanceName":"1"}),"instanceName":"1"});
            var Q619;
            Q619=makeQuery(id+"F11.opPattern","COPY",BODY,{"derivedFrom":makeQuery(id+"F10.opPattern","COPY",BODY,{"derivedFrom":makeQuery(id+"F7.opPattern","COPY",BODY,{"derivedFrom":makeQuery(id+"F6.opPattern","COPY",BODY,{"derivedFrom":makeQuery(id+"F5.opPattern","COPY",BODY,{"derivedFrom":makeQuery(id+"F3.opPattern","COPY",BODY,{"derivedFrom":makeQuery(id+"F2.opPattern","COPY",BODY,{"derivedFrom":makeQuery(id+"F1.opRevolve","SWEPT_BODY",BODY,{"disambiguationData":[OSD([sQuery(id+"F0.wireOp",EDGE,"E1")])]}),"instanceName":"1"}),"instanceName":"1"}),"instanceName":"1"}),"instanceName":"1"}),"instanceName":"1"}),"instanceName":"1"}),"instanceName":"1"});
            var Q620;
            Q620=makeQuery(id+"F11.opPattern","COPY",BODY,{"derivedFrom":makeQuery(id+"F10.opPattern","COPY",BODY,{"derivedFrom":makeQuery(id+"F7.opPattern","COPY",BODY,{"derivedFrom":makeQuery(id+"F6.opPattern","COPY",BODY,{"derivedFrom":makeQuery(id+"F5.opPattern","COPY",BODY,{"derivedFrom":makeQuery(id+"F4.opPattern","COPY",BODY,{"derivedFrom":makeQuery(id+"F1.opRevolve","SWEPT_BODY",BODY,{"disambiguationData":[OSD([sQuery(id+"F0.wireOp",EDGE,"E1")])]}),"instanceName":"1"}),"instanceName":"1"}),"instanceName":"1"}),"instanceName":"1"}),"instanceName":"1"}),"instanceName":"1"});
            var Q621;
            Q621=makeQuery(id+"F11.opPattern","COPY",BODY,{"derivedFrom":makeQuery(id+"F10.opPattern","COPY",BODY,{"derivedFrom":makeQuery(id+"F7.opPattern","COPY",BODY,{"derivedFrom":makeQuery(id+"F6.opPattern","COPY",BODY,{"derivedFrom":makeQuery(id+"F5.opPattern","COPY",BODY,{"derivedFrom":makeQuery(id+"F4.opPattern","COPY",BODY,{"derivedFrom":makeQuery(id+"F2.opPattern","COPY",BODY,{"derivedFrom":makeQuery(id+"F1.opRevolve","SWEPT_BODY",BODY,{"disambiguationData":[OSD([sQuery(id+"F0.wireOp",EDGE,"E1")])]}),"instanceName":"1"}),"instanceName":"1"}),"instanceName":"1"}),"instanceName":"1"}),"instanceName":"1"}),"instanceName":"1"}),"instanceName":"1"});
            var Q622;
            Q622=makeQuery(id+"F11.opPattern","COPY",BODY,{"derivedFrom":makeQuery(id+"F10.opPattern","COPY",BODY,{"derivedFrom":makeQuery(id+"F7.opPattern","COPY",BODY,{"derivedFrom":makeQuery(id+"F6.opPattern","COPY",BODY,{"derivedFrom":makeQuery(id+"F5.opPattern","COPY",BODY,{"derivedFrom":makeQuery(id+"F4.opPattern","COPY",BODY,{"derivedFrom":makeQuery(id+"F3.opPattern","COPY",BODY,{"derivedFrom":makeQuery(id+"F2.opPattern","COPY",BODY,{"derivedFrom":makeQuery(id+"F1.opRevolve","SWEPT_BODY",BODY,{"disambiguationData":[OSD([sQuery(id+"F0.wireOp",EDGE,"E1")])]}),"instanceName":"1"}),"instanceName":"1"}),"instanceName":"1"}),"instanceName":"1"}),"instanceName":"1"}),"instanceName":"1"}),"instanceName":"1"}),"instanceName":"1"});
            var Q623;
            Q623=makeQuery(id+"F11.opPattern","COPY",BODY,{"derivedFrom":makeQuery(id+"F10.opPattern","COPY",BODY,{"derivedFrom":makeQuery(id+"F8.opPattern","COPY",BODY,{"derivedFrom":makeQuery(id+"F1.opRevolve","SWEPT_BODY",BODY,{"disambiguationData":[OSD([sQuery(id+"F0.wireOp",EDGE,"E1")])]}),"instanceName":"1"}),"instanceName":"1"}),"instanceName":"1"});
            var Q624;
            Q624=makeQuery(id+"F11.opPattern","COPY",BODY,{"derivedFrom":makeQuery(id+"F10.opPattern","COPY",BODY,{"derivedFrom":makeQuery(id+"F8.opPattern","COPY",BODY,{"derivedFrom":makeQuery(id+"F2.opPattern","COPY",BODY,{"derivedFrom":makeQuery(id+"F1.opRevolve","SWEPT_BODY",BODY,{"disambiguationData":[OSD([sQuery(id+"F0.wireOp",EDGE,"E1")])]}),"instanceName":"1"}),"instanceName":"1"}),"instanceName":"1"}),"instanceName":"1"});
            var Q625;
            Q625=makeQuery(id+"F11.opPattern","COPY",BODY,{"derivedFrom":makeQuery(id+"F10.opPattern","COPY",BODY,{"derivedFrom":makeQuery(id+"F8.opPattern","COPY",BODY,{"derivedFrom":makeQuery(id+"F3.opPattern","COPY",BODY,{"derivedFrom":makeQuery(id+"F2.opPattern","COPY",BODY,{"derivedFrom":makeQuery(id+"F1.opRevolve","SWEPT_BODY",BODY,{"disambiguationData":[OSD([sQuery(id+"F0.wireOp",EDGE,"E1")])]}),"instanceName":"1"}),"instanceName":"1"}),"instanceName":"1"}),"instanceName":"1"}),"instanceName":"1"});
            var Q626;
            Q626=makeQuery(id+"F11.opPattern","COPY",BODY,{"derivedFrom":makeQuery(id+"F10.opPattern","COPY",BODY,{"derivedFrom":makeQuery(id+"F8.opPattern","COPY",BODY,{"derivedFrom":makeQuery(id+"F4.opPattern","COPY",BODY,{"derivedFrom":makeQuery(id+"F1.opRevolve","SWEPT_BODY",BODY,{"disambiguationData":[OSD([sQuery(id+"F0.wireOp",EDGE,"E1")])]}),"instanceName":"1"}),"instanceName":"1"}),"instanceName":"1"}),"instanceName":"1"});
            var Q627;
            Q627=makeQuery(id+"F11.opPattern","COPY",BODY,{"derivedFrom":makeQuery(id+"F10.opPattern","COPY",BODY,{"derivedFrom":makeQuery(id+"F8.opPattern","COPY",BODY,{"derivedFrom":makeQuery(id+"F4.opPattern","COPY",BODY,{"derivedFrom":makeQuery(id+"F2.opPattern","COPY",BODY,{"derivedFrom":makeQuery(id+"F1.opRevolve","SWEPT_BODY",BODY,{"disambiguationData":[OSD([sQuery(id+"F0.wireOp",EDGE,"E1")])]}),"instanceName":"1"}),"instanceName":"1"}),"instanceName":"1"}),"instanceName":"1"}),"instanceName":"1"});
            var Q628;
            Q628=makeQuery(id+"F11.opPattern","COPY",BODY,{"derivedFrom":makeQuery(id+"F10.opPattern","COPY",BODY,{"derivedFrom":makeQuery(id+"F8.opPattern","COPY",BODY,{"derivedFrom":makeQuery(id+"F4.opPattern","COPY",BODY,{"derivedFrom":makeQuery(id+"F3.opPattern","COPY",BODY,{"derivedFrom":makeQuery(id+"F2.opPattern","COPY",BODY,{"derivedFrom":makeQuery(id+"F1.opRevolve","SWEPT_BODY",BODY,{"disambiguationData":[OSD([sQuery(id+"F0.wireOp",EDGE,"E1")])]}),"instanceName":"1"}),"instanceName":"1"}),"instanceName":"1"}),"instanceName":"1"}),"instanceName":"1"}),"instanceName":"1"});
            var Q629;
            Q629=makeQuery(id+"F11.opPattern","COPY",BODY,{"derivedFrom":makeQuery(id+"F10.opPattern","COPY",BODY,{"derivedFrom":makeQuery(id+"F8.opPattern","COPY",BODY,{"derivedFrom":makeQuery(id+"F5.opPattern","COPY",BODY,{"derivedFrom":makeQuery(id+"F1.opRevolve","SWEPT_BODY",BODY,{"disambiguationData":[OSD([sQuery(id+"F0.wireOp",EDGE,"E1")])]}),"instanceName":"1"}),"instanceName":"1"}),"instanceName":"1"}),"instanceName":"1"});
            var Q630;
            Q630=makeQuery(id+"F11.opPattern","COPY",BODY,{"derivedFrom":makeQuery(id+"F10.opPattern","COPY",BODY,{"derivedFrom":makeQuery(id+"F8.opPattern","COPY",BODY,{"derivedFrom":makeQuery(id+"F5.opPattern","COPY",BODY,{"derivedFrom":makeQuery(id+"F2.opPattern","COPY",BODY,{"derivedFrom":makeQuery(id+"F1.opRevolve","SWEPT_BODY",BODY,{"disambiguationData":[OSD([sQuery(id+"F0.wireOp",EDGE,"E1")])]}),"instanceName":"1"}),"instanceName":"1"}),"instanceName":"1"}),"instanceName":"1"}),"instanceName":"1"});
            var Q631;
            Q631=makeQuery(id+"F11.opPattern","COPY",BODY,{"derivedFrom":makeQuery(id+"F10.opPattern","COPY",BODY,{"derivedFrom":makeQuery(id+"F8.opPattern","COPY",BODY,{"derivedFrom":makeQuery(id+"F5.opPattern","COPY",BODY,{"derivedFrom":makeQuery(id+"F3.opPattern","COPY",BODY,{"derivedFrom":makeQuery(id+"F2.opPattern","COPY",BODY,{"derivedFrom":makeQuery(id+"F1.opRevolve","SWEPT_BODY",BODY,{"disambiguationData":[OSD([sQuery(id+"F0.wireOp",EDGE,"E1")])]}),"instanceName":"1"}),"instanceName":"1"}),"instanceName":"1"}),"instanceName":"1"}),"instanceName":"1"}),"instanceName":"1"});
            var Q632;
            Q632=makeQuery(id+"F11.opPattern","COPY",BODY,{"derivedFrom":makeQuery(id+"F10.opPattern","COPY",BODY,{"derivedFrom":makeQuery(id+"F8.opPattern","COPY",BODY,{"derivedFrom":makeQuery(id+"F5.opPattern","COPY",BODY,{"derivedFrom":makeQuery(id+"F4.opPattern","COPY",BODY,{"derivedFrom":makeQuery(id+"F1.opRevolve","SWEPT_BODY",BODY,{"disambiguationData":[OSD([sQuery(id+"F0.wireOp",EDGE,"E1")])]}),"instanceName":"1"}),"instanceName":"1"}),"instanceName":"1"}),"instanceName":"1"}),"instanceName":"1"});
            var Q633;
            Q633=makeQuery(id+"F11.opPattern","COPY",BODY,{"derivedFrom":makeQuery(id+"F10.opPattern","COPY",BODY,{"derivedFrom":makeQuery(id+"F8.opPattern","COPY",BODY,{"derivedFrom":makeQuery(id+"F5.opPattern","COPY",BODY,{"derivedFrom":makeQuery(id+"F4.opPattern","COPY",BODY,{"derivedFrom":makeQuery(id+"F2.opPattern","COPY",BODY,{"derivedFrom":makeQuery(id+"F1.opRevolve","SWEPT_BODY",BODY,{"disambiguationData":[OSD([sQuery(id+"F0.wireOp",EDGE,"E1")])]}),"instanceName":"1"}),"instanceName":"1"}),"instanceName":"1"}),"instanceName":"1"}),"instanceName":"1"}),"instanceName":"1"});
            var Q634;
            Q634=makeQuery(id+"F11.opPattern","COPY",BODY,{"derivedFrom":makeQuery(id+"F10.opPattern","COPY",BODY,{"derivedFrom":makeQuery(id+"F8.opPattern","COPY",BODY,{"derivedFrom":makeQuery(id+"F5.opPattern","COPY",BODY,{"derivedFrom":makeQuery(id+"F4.opPattern","COPY",BODY,{"derivedFrom":makeQuery(id+"F3.opPattern","COPY",BODY,{"derivedFrom":makeQuery(id+"F2.opPattern","COPY",BODY,{"derivedFrom":makeQuery(id+"F1.opRevolve","SWEPT_BODY",BODY,{"disambiguationData":[OSD([sQuery(id+"F0.wireOp",EDGE,"E1")])]}),"instanceName":"1"}),"instanceName":"1"}),"instanceName":"1"}),"instanceName":"1"}),"instanceName":"1"}),"instanceName":"1"}),"instanceName":"1"});
            var Q635;
            Q635=makeQuery(id+"F11.opPattern","COPY",BODY,{"derivedFrom":makeQuery(id+"F10.opPattern","COPY",BODY,{"derivedFrom":makeQuery(id+"F8.opPattern","COPY",BODY,{"derivedFrom":makeQuery(id+"F6.opPattern","COPY",BODY,{"derivedFrom":makeQuery(id+"F1.opRevolve","SWEPT_BODY",BODY,{"disambiguationData":[OSD([sQuery(id+"F0.wireOp",EDGE,"E1")])]}),"instanceName":"1"}),"instanceName":"1"}),"instanceName":"1"}),"instanceName":"1"});
            var Q636;
            Q636=makeQuery(id+"F11.opPattern","COPY",BODY,{"derivedFrom":makeQuery(id+"F10.opPattern","COPY",BODY,{"derivedFrom":makeQuery(id+"F8.opPattern","COPY",BODY,{"derivedFrom":makeQuery(id+"F6.opPattern","COPY",BODY,{"derivedFrom":makeQuery(id+"F2.opPattern","COPY",BODY,{"derivedFrom":makeQuery(id+"F1.opRevolve","SWEPT_BODY",BODY,{"disambiguationData":[OSD([sQuery(id+"F0.wireOp",EDGE,"E1")])]}),"instanceName":"1"}),"instanceName":"1"}),"instanceName":"1"}),"instanceName":"1"}),"instanceName":"1"});
            var Q637;
            Q637=makeQuery(id+"F11.opPattern","COPY",BODY,{"derivedFrom":makeQuery(id+"F10.opPattern","COPY",BODY,{"derivedFrom":makeQuery(id+"F8.opPattern","COPY",BODY,{"derivedFrom":makeQuery(id+"F6.opPattern","COPY",BODY,{"derivedFrom":makeQuery(id+"F3.opPattern","COPY",BODY,{"derivedFrom":makeQuery(id+"F2.opPattern","COPY",BODY,{"derivedFrom":makeQuery(id+"F1.opRevolve","SWEPT_BODY",BODY,{"disambiguationData":[OSD([sQuery(id+"F0.wireOp",EDGE,"E1")])]}),"instanceName":"1"}),"instanceName":"1"}),"instanceName":"1"}),"instanceName":"1"}),"instanceName":"1"}),"instanceName":"1"});
            var Q638;
            Q638=makeQuery(id+"F11.opPattern","COPY",BODY,{"derivedFrom":makeQuery(id+"F10.opPattern","COPY",BODY,{"derivedFrom":makeQuery(id+"F8.opPattern","COPY",BODY,{"derivedFrom":makeQuery(id+"F6.opPattern","COPY",BODY,{"derivedFrom":makeQuery(id+"F4.opPattern","COPY",BODY,{"derivedFrom":makeQuery(id+"F1.opRevolve","SWEPT_BODY",BODY,{"disambiguationData":[OSD([sQuery(id+"F0.wireOp",EDGE,"E1")])]}),"instanceName":"1"}),"instanceName":"1"}),"instanceName":"1"}),"instanceName":"1"}),"instanceName":"1"});
            var Q639;
            Q639=makeQuery(id+"F11.opPattern","COPY",BODY,{"derivedFrom":makeQuery(id+"F10.opPattern","COPY",BODY,{"derivedFrom":makeQuery(id+"F8.opPattern","COPY",BODY,{"derivedFrom":makeQuery(id+"F6.opPattern","COPY",BODY,{"derivedFrom":makeQuery(id+"F4.opPattern","COPY",BODY,{"derivedFrom":makeQuery(id+"F2.opPattern","COPY",BODY,{"derivedFrom":makeQuery(id+"F1.opRevolve","SWEPT_BODY",BODY,{"disambiguationData":[OSD([sQuery(id+"F0.wireOp",EDGE,"E1")])]}),"instanceName":"1"}),"instanceName":"1"}),"instanceName":"1"}),"instanceName":"1"}),"instanceName":"1"}),"instanceName":"1"});
            var Q640;
            Q640=makeQuery(id+"F11.opPattern","COPY",BODY,{"derivedFrom":makeQuery(id+"F10.opPattern","COPY",BODY,{"derivedFrom":makeQuery(id+"F8.opPattern","COPY",BODY,{"derivedFrom":makeQuery(id+"F6.opPattern","COPY",BODY,{"derivedFrom":makeQuery(id+"F4.opPattern","COPY",BODY,{"derivedFrom":makeQuery(id+"F3.opPattern","COPY",BODY,{"derivedFrom":makeQuery(id+"F2.opPattern","COPY",BODY,{"derivedFrom":makeQuery(id+"F1.opRevolve","SWEPT_BODY",BODY,{"disambiguationData":[OSD([sQuery(id+"F0.wireOp",EDGE,"E1")])]}),"instanceName":"1"}),"instanceName":"1"}),"instanceName":"1"}),"instanceName":"1"}),"instanceName":"1"}),"instanceName":"1"}),"instanceName":"1"});
            var Q641;
            Q641=makeQuery(id+"F11.opPattern","COPY",BODY,{"derivedFrom":makeQuery(id+"F10.opPattern","COPY",BODY,{"derivedFrom":makeQuery(id+"F8.opPattern","COPY",BODY,{"derivedFrom":makeQuery(id+"F6.opPattern","COPY",BODY,{"derivedFrom":makeQuery(id+"F5.opPattern","COPY",BODY,{"derivedFrom":makeQuery(id+"F1.opRevolve","SWEPT_BODY",BODY,{"disambiguationData":[OSD([sQuery(id+"F0.wireOp",EDGE,"E1")])]}),"instanceName":"1"}),"instanceName":"1"}),"instanceName":"1"}),"instanceName":"1"}),"instanceName":"1"});
            var Q642;
            Q642=makeQuery(id+"F11.opPattern","COPY",BODY,{"derivedFrom":makeQuery(id+"F10.opPattern","COPY",BODY,{"derivedFrom":makeQuery(id+"F8.opPattern","COPY",BODY,{"derivedFrom":makeQuery(id+"F6.opPattern","COPY",BODY,{"derivedFrom":makeQuery(id+"F5.opPattern","COPY",BODY,{"derivedFrom":makeQuery(id+"F2.opPattern","COPY",BODY,{"derivedFrom":makeQuery(id+"F1.opRevolve","SWEPT_BODY",BODY,{"disambiguationData":[OSD([sQuery(id+"F0.wireOp",EDGE,"E1")])]}),"instanceName":"1"}),"instanceName":"1"}),"instanceName":"1"}),"instanceName":"1"}),"instanceName":"1"}),"instanceName":"1"});
            var Q643;
            Q643=makeQuery(id+"F11.opPattern","COPY",BODY,{"derivedFrom":makeQuery(id+"F10.opPattern","COPY",BODY,{"derivedFrom":makeQuery(id+"F8.opPattern","COPY",BODY,{"derivedFrom":makeQuery(id+"F6.opPattern","COPY",BODY,{"derivedFrom":makeQuery(id+"F5.opPattern","COPY",BODY,{"derivedFrom":makeQuery(id+"F3.opPattern","COPY",BODY,{"derivedFrom":makeQuery(id+"F2.opPattern","COPY",BODY,{"derivedFrom":makeQuery(id+"F1.opRevolve","SWEPT_BODY",BODY,{"disambiguationData":[OSD([sQuery(id+"F0.wireOp",EDGE,"E1")])]}),"instanceName":"1"}),"instanceName":"1"}),"instanceName":"1"}),"instanceName":"1"}),"instanceName":"1"}),"instanceName":"1"}),"instanceName":"1"});
            var Q644;
            Q644=makeQuery(id+"F11.opPattern","COPY",BODY,{"derivedFrom":makeQuery(id+"F10.opPattern","COPY",BODY,{"derivedFrom":makeQuery(id+"F8.opPattern","COPY",BODY,{"derivedFrom":makeQuery(id+"F6.opPattern","COPY",BODY,{"derivedFrom":makeQuery(id+"F5.opPattern","COPY",BODY,{"derivedFrom":makeQuery(id+"F4.opPattern","COPY",BODY,{"derivedFrom":makeQuery(id+"F1.opRevolve","SWEPT_BODY",BODY,{"disambiguationData":[OSD([sQuery(id+"F0.wireOp",EDGE,"E1")])]}),"instanceName":"1"}),"instanceName":"1"}),"instanceName":"1"}),"instanceName":"1"}),"instanceName":"1"}),"instanceName":"1"});
            var Q645;
            Q645=makeQuery(id+"F11.opPattern","COPY",BODY,{"derivedFrom":makeQuery(id+"F10.opPattern","COPY",BODY,{"derivedFrom":makeQuery(id+"F8.opPattern","COPY",BODY,{"derivedFrom":makeQuery(id+"F6.opPattern","COPY",BODY,{"derivedFrom":makeQuery(id+"F5.opPattern","COPY",BODY,{"derivedFrom":makeQuery(id+"F4.opPattern","COPY",BODY,{"derivedFrom":makeQuery(id+"F2.opPattern","COPY",BODY,{"derivedFrom":makeQuery(id+"F1.opRevolve","SWEPT_BODY",BODY,{"disambiguationData":[OSD([sQuery(id+"F0.wireOp",EDGE,"E1")])]}),"instanceName":"1"}),"instanceName":"1"}),"instanceName":"1"}),"instanceName":"1"}),"instanceName":"1"}),"instanceName":"1"}),"instanceName":"1"});
            var Q646;
            Q646=makeQuery(id+"F11.opPattern","COPY",BODY,{"derivedFrom":makeQuery(id+"F10.opPattern","COPY",BODY,{"derivedFrom":makeQuery(id+"F8.opPattern","COPY",BODY,{"derivedFrom":makeQuery(id+"F6.opPattern","COPY",BODY,{"derivedFrom":makeQuery(id+"F5.opPattern","COPY",BODY,{"derivedFrom":makeQuery(id+"F4.opPattern","COPY",BODY,{"derivedFrom":makeQuery(id+"F3.opPattern","COPY",BODY,{"derivedFrom":makeQuery(id+"F2.opPattern","COPY",BODY,{"derivedFrom":makeQuery(id+"F1.opRevolve","SWEPT_BODY",BODY,{"disambiguationData":[OSD([sQuery(id+"F0.wireOp",EDGE,"E1")])]}),"instanceName":"1"}),"instanceName":"1"}),"instanceName":"1"}),"instanceName":"1"}),"instanceName":"1"}),"instanceName":"1"}),"instanceName":"1"}),"instanceName":"1"});
            var Q647;
            Q647=makeQuery(id+"F11.opPattern","COPY",BODY,{"derivedFrom":makeQuery(id+"F10.opPattern","COPY",BODY,{"derivedFrom":makeQuery(id+"F8.opPattern","COPY",BODY,{"derivedFrom":makeQuery(id+"F7.opPattern","COPY",BODY,{"derivedFrom":makeQuery(id+"F1.opRevolve","SWEPT_BODY",BODY,{"disambiguationData":[OSD([sQuery(id+"F0.wireOp",EDGE,"E1")])]}),"instanceName":"1"}),"instanceName":"1"}),"instanceName":"1"}),"instanceName":"1"});
            var Q648;
            Q648=makeQuery(id+"F11.opPattern","COPY",BODY,{"derivedFrom":makeQuery(id+"F10.opPattern","COPY",BODY,{"derivedFrom":makeQuery(id+"F8.opPattern","COPY",BODY,{"derivedFrom":makeQuery(id+"F7.opPattern","COPY",BODY,{"derivedFrom":makeQuery(id+"F2.opPattern","COPY",BODY,{"derivedFrom":makeQuery(id+"F1.opRevolve","SWEPT_BODY",BODY,{"disambiguationData":[OSD([sQuery(id+"F0.wireOp",EDGE,"E1")])]}),"instanceName":"1"}),"instanceName":"1"}),"instanceName":"1"}),"instanceName":"1"}),"instanceName":"1"});
            var Q649;
            Q649=makeQuery(id+"F11.opPattern","COPY",BODY,{"derivedFrom":makeQuery(id+"F10.opPattern","COPY",BODY,{"derivedFrom":makeQuery(id+"F8.opPattern","COPY",BODY,{"derivedFrom":makeQuery(id+"F7.opPattern","COPY",BODY,{"derivedFrom":makeQuery(id+"F3.opPattern","COPY",BODY,{"derivedFrom":makeQuery(id+"F2.opPattern","COPY",BODY,{"derivedFrom":makeQuery(id+"F1.opRevolve","SWEPT_BODY",BODY,{"disambiguationData":[OSD([sQuery(id+"F0.wireOp",EDGE,"E1")])]}),"instanceName":"1"}),"instanceName":"1"}),"instanceName":"1"}),"instanceName":"1"}),"instanceName":"1"}),"instanceName":"1"});
            var Q650;
            Q650=makeQuery(id+"F11.opPattern","COPY",BODY,{"derivedFrom":makeQuery(id+"F10.opPattern","COPY",BODY,{"derivedFrom":makeQuery(id+"F8.opPattern","COPY",BODY,{"derivedFrom":makeQuery(id+"F7.opPattern","COPY",BODY,{"derivedFrom":makeQuery(id+"F4.opPattern","COPY",BODY,{"derivedFrom":makeQuery(id+"F1.opRevolve","SWEPT_BODY",BODY,{"disambiguationData":[OSD([sQuery(id+"F0.wireOp",EDGE,"E1")])]}),"instanceName":"1"}),"instanceName":"1"}),"instanceName":"1"}),"instanceName":"1"}),"instanceName":"1"});
            var Q651;
            Q651=makeQuery(id+"F11.opPattern","COPY",BODY,{"derivedFrom":makeQuery(id+"F10.opPattern","COPY",BODY,{"derivedFrom":makeQuery(id+"F8.opPattern","COPY",BODY,{"derivedFrom":makeQuery(id+"F7.opPattern","COPY",BODY,{"derivedFrom":makeQuery(id+"F4.opPattern","COPY",BODY,{"derivedFrom":makeQuery(id+"F2.opPattern","COPY",BODY,{"derivedFrom":makeQuery(id+"F1.opRevolve","SWEPT_BODY",BODY,{"disambiguationData":[OSD([sQuery(id+"F0.wireOp",EDGE,"E1")])]}),"instanceName":"1"}),"instanceName":"1"}),"instanceName":"1"}),"instanceName":"1"}),"instanceName":"1"}),"instanceName":"1"});
            var Q652;
            Q652=makeQuery(id+"F11.opPattern","COPY",BODY,{"derivedFrom":makeQuery(id+"F10.opPattern","COPY",BODY,{"derivedFrom":makeQuery(id+"F8.opPattern","COPY",BODY,{"derivedFrom":makeQuery(id+"F7.opPattern","COPY",BODY,{"derivedFrom":makeQuery(id+"F4.opPattern","COPY",BODY,{"derivedFrom":makeQuery(id+"F3.opPattern","COPY",BODY,{"derivedFrom":makeQuery(id+"F2.opPattern","COPY",BODY,{"derivedFrom":makeQuery(id+"F1.opRevolve","SWEPT_BODY",BODY,{"disambiguationData":[OSD([sQuery(id+"F0.wireOp",EDGE,"E1")])]}),"instanceName":"1"}),"instanceName":"1"}),"instanceName":"1"}),"instanceName":"1"}),"instanceName":"1"}),"instanceName":"1"}),"instanceName":"1"});
            var Q653;
            Q653=makeQuery(id+"F11.opPattern","COPY",BODY,{"derivedFrom":makeQuery(id+"F10.opPattern","COPY",BODY,{"derivedFrom":makeQuery(id+"F8.opPattern","COPY",BODY,{"derivedFrom":makeQuery(id+"F7.opPattern","COPY",BODY,{"derivedFrom":makeQuery(id+"F5.opPattern","COPY",BODY,{"derivedFrom":makeQuery(id+"F1.opRevolve","SWEPT_BODY",BODY,{"disambiguationData":[OSD([sQuery(id+"F0.wireOp",EDGE,"E1")])]}),"instanceName":"1"}),"instanceName":"1"}),"instanceName":"1"}),"instanceName":"1"}),"instanceName":"1"});
            var Q654;
            Q654=makeQuery(id+"F11.opPattern","COPY",BODY,{"derivedFrom":makeQuery(id+"F10.opPattern","COPY",BODY,{"derivedFrom":makeQuery(id+"F8.opPattern","COPY",BODY,{"derivedFrom":makeQuery(id+"F7.opPattern","COPY",BODY,{"derivedFrom":makeQuery(id+"F5.opPattern","COPY",BODY,{"derivedFrom":makeQuery(id+"F2.opPattern","COPY",BODY,{"derivedFrom":makeQuery(id+"F1.opRevolve","SWEPT_BODY",BODY,{"disambiguationData":[OSD([sQuery(id+"F0.wireOp",EDGE,"E1")])]}),"instanceName":"1"}),"instanceName":"1"}),"instanceName":"1"}),"instanceName":"1"}),"instanceName":"1"}),"instanceName":"1"});
            var Q655;
            Q655=makeQuery(id+"F11.opPattern","COPY",BODY,{"derivedFrom":makeQuery(id+"F10.opPattern","COPY",BODY,{"derivedFrom":makeQuery(id+"F8.opPattern","COPY",BODY,{"derivedFrom":makeQuery(id+"F7.opPattern","COPY",BODY,{"derivedFrom":makeQuery(id+"F5.opPattern","COPY",BODY,{"derivedFrom":makeQuery(id+"F3.opPattern","COPY",BODY,{"derivedFrom":makeQuery(id+"F2.opPattern","COPY",BODY,{"derivedFrom":makeQuery(id+"F1.opRevolve","SWEPT_BODY",BODY,{"disambiguationData":[OSD([sQuery(id+"F0.wireOp",EDGE,"E1")])]}),"instanceName":"1"}),"instanceName":"1"}),"instanceName":"1"}),"instanceName":"1"}),"instanceName":"1"}),"instanceName":"1"}),"instanceName":"1"});
            var Q656;
            Q656=makeQuery(id+"F11.opPattern","COPY",BODY,{"derivedFrom":makeQuery(id+"F10.opPattern","COPY",BODY,{"derivedFrom":makeQuery(id+"F8.opPattern","COPY",BODY,{"derivedFrom":makeQuery(id+"F7.opPattern","COPY",BODY,{"derivedFrom":makeQuery(id+"F5.opPattern","COPY",BODY,{"derivedFrom":makeQuery(id+"F4.opPattern","COPY",BODY,{"derivedFrom":makeQuery(id+"F1.opRevolve","SWEPT_BODY",BODY,{"disambiguationData":[OSD([sQuery(id+"F0.wireOp",EDGE,"E1")])]}),"instanceName":"1"}),"instanceName":"1"}),"instanceName":"1"}),"instanceName":"1"}),"instanceName":"1"}),"instanceName":"1"});
            var Q657;
            Q657=makeQuery(id+"F11.opPattern","COPY",BODY,{"derivedFrom":makeQuery(id+"F10.opPattern","COPY",BODY,{"derivedFrom":makeQuery(id+"F8.opPattern","COPY",BODY,{"derivedFrom":makeQuery(id+"F7.opPattern","COPY",BODY,{"derivedFrom":makeQuery(id+"F5.opPattern","COPY",BODY,{"derivedFrom":makeQuery(id+"F4.opPattern","COPY",BODY,{"derivedFrom":makeQuery(id+"F2.opPattern","COPY",BODY,{"derivedFrom":makeQuery(id+"F1.opRevolve","SWEPT_BODY",BODY,{"disambiguationData":[OSD([sQuery(id+"F0.wireOp",EDGE,"E1")])]}),"instanceName":"1"}),"instanceName":"1"}),"instanceName":"1"}),"instanceName":"1"}),"instanceName":"1"}),"instanceName":"1"}),"instanceName":"1"});
            var Q658;
            Q658=makeQuery(id+"F11.opPattern","COPY",BODY,{"derivedFrom":makeQuery(id+"F10.opPattern","COPY",BODY,{"derivedFrom":makeQuery(id+"F8.opPattern","COPY",BODY,{"derivedFrom":makeQuery(id+"F7.opPattern","COPY",BODY,{"derivedFrom":makeQuery(id+"F5.opPattern","COPY",BODY,{"derivedFrom":makeQuery(id+"F4.opPattern","COPY",BODY,{"derivedFrom":makeQuery(id+"F3.opPattern","COPY",BODY,{"derivedFrom":makeQuery(id+"F2.opPattern","COPY",BODY,{"derivedFrom":makeQuery(id+"F1.opRevolve","SWEPT_BODY",BODY,{"disambiguationData":[OSD([sQuery(id+"F0.wireOp",EDGE,"E1")])]}),"instanceName":"1"}),"instanceName":"1"}),"instanceName":"1"}),"instanceName":"1"}),"instanceName":"1"}),"instanceName":"1"}),"instanceName":"1"}),"instanceName":"1"});
            var Q659;
            Q659=makeQuery(id+"F11.opPattern","COPY",BODY,{"derivedFrom":makeQuery(id+"F10.opPattern","COPY",BODY,{"derivedFrom":makeQuery(id+"F8.opPattern","COPY",BODY,{"derivedFrom":makeQuery(id+"F7.opPattern","COPY",BODY,{"derivedFrom":makeQuery(id+"F6.opPattern","COPY",BODY,{"derivedFrom":makeQuery(id+"F1.opRevolve","SWEPT_BODY",BODY,{"disambiguationData":[OSD([sQuery(id+"F0.wireOp",EDGE,"E1")])]}),"instanceName":"1"}),"instanceName":"1"}),"instanceName":"1"}),"instanceName":"1"}),"instanceName":"1"});
            var Q660;
            Q660=makeQuery(id+"F11.opPattern","COPY",BODY,{"derivedFrom":makeQuery(id+"F10.opPattern","COPY",BODY,{"derivedFrom":makeQuery(id+"F8.opPattern","COPY",BODY,{"derivedFrom":makeQuery(id+"F7.opPattern","COPY",BODY,{"derivedFrom":makeQuery(id+"F6.opPattern","COPY",BODY,{"derivedFrom":makeQuery(id+"F2.opPattern","COPY",BODY,{"derivedFrom":makeQuery(id+"F1.opRevolve","SWEPT_BODY",BODY,{"disambiguationData":[OSD([sQuery(id+"F0.wireOp",EDGE,"E1")])]}),"instanceName":"1"}),"instanceName":"1"}),"instanceName":"1"}),"instanceName":"1"}),"instanceName":"1"}),"instanceName":"1"});
            var Q661;
            Q661=makeQuery(id+"F11.opPattern","COPY",BODY,{"derivedFrom":makeQuery(id+"F10.opPattern","COPY",BODY,{"derivedFrom":makeQuery(id+"F8.opPattern","COPY",BODY,{"derivedFrom":makeQuery(id+"F7.opPattern","COPY",BODY,{"derivedFrom":makeQuery(id+"F6.opPattern","COPY",BODY,{"derivedFrom":makeQuery(id+"F3.opPattern","COPY",BODY,{"derivedFrom":makeQuery(id+"F2.opPattern","COPY",BODY,{"derivedFrom":makeQuery(id+"F1.opRevolve","SWEPT_BODY",BODY,{"disambiguationData":[OSD([sQuery(id+"F0.wireOp",EDGE,"E1")])]}),"instanceName":"1"}),"instanceName":"1"}),"instanceName":"1"}),"instanceName":"1"}),"instanceName":"1"}),"instanceName":"1"}),"instanceName":"1"});
            var Q662;
            Q662=makeQuery(id+"F11.opPattern","COPY",BODY,{"derivedFrom":makeQuery(id+"F10.opPattern","COPY",BODY,{"derivedFrom":makeQuery(id+"F8.opPattern","COPY",BODY,{"derivedFrom":makeQuery(id+"F7.opPattern","COPY",BODY,{"derivedFrom":makeQuery(id+"F6.opPattern","COPY",BODY,{"derivedFrom":makeQuery(id+"F4.opPattern","COPY",BODY,{"derivedFrom":makeQuery(id+"F1.opRevolve","SWEPT_BODY",BODY,{"disambiguationData":[OSD([sQuery(id+"F0.wireOp",EDGE,"E1")])]}),"instanceName":"1"}),"instanceName":"1"}),"instanceName":"1"}),"instanceName":"1"}),"instanceName":"1"}),"instanceName":"1"});
            var Q663;
            Q663=makeQuery(id+"F11.opPattern","COPY",BODY,{"derivedFrom":makeQuery(id+"F10.opPattern","COPY",BODY,{"derivedFrom":makeQuery(id+"F8.opPattern","COPY",BODY,{"derivedFrom":makeQuery(id+"F7.opPattern","COPY",BODY,{"derivedFrom":makeQuery(id+"F6.opPattern","COPY",BODY,{"derivedFrom":makeQuery(id+"F4.opPattern","COPY",BODY,{"derivedFrom":makeQuery(id+"F2.opPattern","COPY",BODY,{"derivedFrom":makeQuery(id+"F1.opRevolve","SWEPT_BODY",BODY,{"disambiguationData":[OSD([sQuery(id+"F0.wireOp",EDGE,"E1")])]}),"instanceName":"1"}),"instanceName":"1"}),"instanceName":"1"}),"instanceName":"1"}),"instanceName":"1"}),"instanceName":"1"}),"instanceName":"1"});
            var Q664;
            Q664=makeQuery(id+"F11.opPattern","COPY",BODY,{"derivedFrom":makeQuery(id+"F10.opPattern","COPY",BODY,{"derivedFrom":makeQuery(id+"F8.opPattern","COPY",BODY,{"derivedFrom":makeQuery(id+"F7.opPattern","COPY",BODY,{"derivedFrom":makeQuery(id+"F6.opPattern","COPY",BODY,{"derivedFrom":makeQuery(id+"F4.opPattern","COPY",BODY,{"derivedFrom":makeQuery(id+"F3.opPattern","COPY",BODY,{"derivedFrom":makeQuery(id+"F2.opPattern","COPY",BODY,{"derivedFrom":makeQuery(id+"F1.opRevolve","SWEPT_BODY",BODY,{"disambiguationData":[OSD([sQuery(id+"F0.wireOp",EDGE,"E1")])]}),"instanceName":"1"}),"instanceName":"1"}),"instanceName":"1"}),"instanceName":"1"}),"instanceName":"1"}),"instanceName":"1"}),"instanceName":"1"}),"instanceName":"1"});
            var Q665;
            Q665=makeQuery(id+"F11.opPattern","COPY",BODY,{"derivedFrom":makeQuery(id+"F10.opPattern","COPY",BODY,{"derivedFrom":makeQuery(id+"F8.opPattern","COPY",BODY,{"derivedFrom":makeQuery(id+"F7.opPattern","COPY",BODY,{"derivedFrom":makeQuery(id+"F6.opPattern","COPY",BODY,{"derivedFrom":makeQuery(id+"F5.opPattern","COPY",BODY,{"derivedFrom":makeQuery(id+"F1.opRevolve","SWEPT_BODY",BODY,{"disambiguationData":[OSD([sQuery(id+"F0.wireOp",EDGE,"E1")])]}),"instanceName":"1"}),"instanceName":"1"}),"instanceName":"1"}),"instanceName":"1"}),"instanceName":"1"}),"instanceName":"1"});
            var Q666;
            Q666=makeQuery(id+"F11.opPattern","COPY",BODY,{"derivedFrom":makeQuery(id+"F10.opPattern","COPY",BODY,{"derivedFrom":makeQuery(id+"F8.opPattern","COPY",BODY,{"derivedFrom":makeQuery(id+"F7.opPattern","COPY",BODY,{"derivedFrom":makeQuery(id+"F6.opPattern","COPY",BODY,{"derivedFrom":makeQuery(id+"F5.opPattern","COPY",BODY,{"derivedFrom":makeQuery(id+"F2.opPattern","COPY",BODY,{"derivedFrom":makeQuery(id+"F1.opRevolve","SWEPT_BODY",BODY,{"disambiguationData":[OSD([sQuery(id+"F0.wireOp",EDGE,"E1")])]}),"instanceName":"1"}),"instanceName":"1"}),"instanceName":"1"}),"instanceName":"1"}),"instanceName":"1"}),"instanceName":"1"}),"instanceName":"1"});
            var Q667;
            Q667=makeQuery(id+"F11.opPattern","COPY",BODY,{"derivedFrom":makeQuery(id+"F10.opPattern","COPY",BODY,{"derivedFrom":makeQuery(id+"F8.opPattern","COPY",BODY,{"derivedFrom":makeQuery(id+"F7.opPattern","COPY",BODY,{"derivedFrom":makeQuery(id+"F6.opPattern","COPY",BODY,{"derivedFrom":makeQuery(id+"F5.opPattern","COPY",BODY,{"derivedFrom":makeQuery(id+"F3.opPattern","COPY",BODY,{"derivedFrom":makeQuery(id+"F2.opPattern","COPY",BODY,{"derivedFrom":makeQuery(id+"F1.opRevolve","SWEPT_BODY",BODY,{"disambiguationData":[OSD([sQuery(id+"F0.wireOp",EDGE,"E1")])]}),"instanceName":"1"}),"instanceName":"1"}),"instanceName":"1"}),"instanceName":"1"}),"instanceName":"1"}),"instanceName":"1"}),"instanceName":"1"}),"instanceName":"1"});
            var Q668;
            Q668=makeQuery(id+"F11.opPattern","COPY",BODY,{"derivedFrom":makeQuery(id+"F10.opPattern","COPY",BODY,{"derivedFrom":makeQuery(id+"F8.opPattern","COPY",BODY,{"derivedFrom":makeQuery(id+"F7.opPattern","COPY",BODY,{"derivedFrom":makeQuery(id+"F6.opPattern","COPY",BODY,{"derivedFrom":makeQuery(id+"F5.opPattern","COPY",BODY,{"derivedFrom":makeQuery(id+"F4.opPattern","COPY",BODY,{"derivedFrom":makeQuery(id+"F1.opRevolve","SWEPT_BODY",BODY,{"disambiguationData":[OSD([sQuery(id+"F0.wireOp",EDGE,"E1")])]}),"instanceName":"1"}),"instanceName":"1"}),"instanceName":"1"}),"instanceName":"1"}),"instanceName":"1"}),"instanceName":"1"}),"instanceName":"1"});
            var Q669;
            Q669=makeQuery(id+"F11.opPattern","COPY",BODY,{"derivedFrom":makeQuery(id+"F10.opPattern","COPY",BODY,{"derivedFrom":makeQuery(id+"F8.opPattern","COPY",BODY,{"derivedFrom":makeQuery(id+"F7.opPattern","COPY",BODY,{"derivedFrom":makeQuery(id+"F6.opPattern","COPY",BODY,{"derivedFrom":makeQuery(id+"F5.opPattern","COPY",BODY,{"derivedFrom":makeQuery(id+"F4.opPattern","COPY",BODY,{"derivedFrom":makeQuery(id+"F2.opPattern","COPY",BODY,{"derivedFrom":makeQuery(id+"F1.opRevolve","SWEPT_BODY",BODY,{"disambiguationData":[OSD([sQuery(id+"F0.wireOp",EDGE,"E1")])]}),"instanceName":"1"}),"instanceName":"1"}),"instanceName":"1"}),"instanceName":"1"}),"instanceName":"1"}),"instanceName":"1"}),"instanceName":"1"}),"instanceName":"1"});
            var Q670;
            Q670=makeQuery(id+"F11.opPattern","COPY",BODY,{"derivedFrom":makeQuery(id+"F10.opPattern","COPY",BODY,{"derivedFrom":makeQuery(id+"F8.opPattern","COPY",BODY,{"derivedFrom":makeQuery(id+"F7.opPattern","COPY",BODY,{"derivedFrom":makeQuery(id+"F6.opPattern","COPY",BODY,{"derivedFrom":makeQuery(id+"F5.opPattern","COPY",BODY,{"derivedFrom":makeQuery(id+"F4.opPattern","COPY",BODY,{"derivedFrom":makeQuery(id+"F3.opPattern","COPY",BODY,{"derivedFrom":makeQuery(id+"F2.opPattern","COPY",BODY,{"derivedFrom":makeQuery(id+"F1.opRevolve","SWEPT_BODY",BODY,{"disambiguationData":[OSD([sQuery(id+"F0.wireOp",EDGE,"E1")])]}),"instanceName":"1"}),"instanceName":"1"}),"instanceName":"1"}),"instanceName":"1"}),"instanceName":"1"}),"instanceName":"1"}),"instanceName":"1"}),"instanceName":"1"}),"instanceName":"1"});
            var Q671;
            Q671=makeQuery(id+"F11.opPattern","COPY",BODY,{"derivedFrom":makeQuery(id+"F10.opPattern","COPY",BODY,{"derivedFrom":makeQuery(id+"F9.opPattern","COPY",BODY,{"derivedFrom":makeQuery(id+"F1.opRevolve","SWEPT_BODY",BODY,{"disambiguationData":[OSD([sQuery(id+"F0.wireOp",EDGE,"E1")])]}),"instanceName":"1"}),"instanceName":"1"}),"instanceName":"1"});
            var Q672;
            Q672=makeQuery(id+"F11.opPattern","COPY",BODY,{"derivedFrom":makeQuery(id+"F10.opPattern","COPY",BODY,{"derivedFrom":makeQuery(id+"F9.opPattern","COPY",BODY,{"derivedFrom":makeQuery(id+"F2.opPattern","COPY",BODY,{"derivedFrom":makeQuery(id+"F1.opRevolve","SWEPT_BODY",BODY,{"disambiguationData":[OSD([sQuery(id+"F0.wireOp",EDGE,"E1")])]}),"instanceName":"1"}),"instanceName":"1"}),"instanceName":"1"}),"instanceName":"1"});
            var Q673;
            Q673=makeQuery(id+"F11.opPattern","COPY",BODY,{"derivedFrom":makeQuery(id+"F10.opPattern","COPY",BODY,{"derivedFrom":makeQuery(id+"F9.opPattern","COPY",BODY,{"derivedFrom":makeQuery(id+"F3.opPattern","COPY",BODY,{"derivedFrom":makeQuery(id+"F2.opPattern","COPY",BODY,{"derivedFrom":makeQuery(id+"F1.opRevolve","SWEPT_BODY",BODY,{"disambiguationData":[OSD([sQuery(id+"F0.wireOp",EDGE,"E1")])]}),"instanceName":"1"}),"instanceName":"1"}),"instanceName":"1"}),"instanceName":"1"}),"instanceName":"1"});
            var Q674;
            Q674=makeQuery(id+"F11.opPattern","COPY",BODY,{"derivedFrom":makeQuery(id+"F10.opPattern","COPY",BODY,{"derivedFrom":makeQuery(id+"F9.opPattern","COPY",BODY,{"derivedFrom":makeQuery(id+"F4.opPattern","COPY",BODY,{"derivedFrom":makeQuery(id+"F1.opRevolve","SWEPT_BODY",BODY,{"disambiguationData":[OSD([sQuery(id+"F0.wireOp",EDGE,"E1")])]}),"instanceName":"1"}),"instanceName":"1"}),"instanceName":"1"}),"instanceName":"1"});
            var Q675;
            Q675=makeQuery(id+"F11.opPattern","COPY",BODY,{"derivedFrom":makeQuery(id+"F10.opPattern","COPY",BODY,{"derivedFrom":makeQuery(id+"F9.opPattern","COPY",BODY,{"derivedFrom":makeQuery(id+"F4.opPattern","COPY",BODY,{"derivedFrom":makeQuery(id+"F2.opPattern","COPY",BODY,{"derivedFrom":makeQuery(id+"F1.opRevolve","SWEPT_BODY",BODY,{"disambiguationData":[OSD([sQuery(id+"F0.wireOp",EDGE,"E1")])]}),"instanceName":"1"}),"instanceName":"1"}),"instanceName":"1"}),"instanceName":"1"}),"instanceName":"1"});
            var Q676;
            Q676=makeQuery(id+"F11.opPattern","COPY",BODY,{"derivedFrom":makeQuery(id+"F10.opPattern","COPY",BODY,{"derivedFrom":makeQuery(id+"F9.opPattern","COPY",BODY,{"derivedFrom":makeQuery(id+"F4.opPattern","COPY",BODY,{"derivedFrom":makeQuery(id+"F3.opPattern","COPY",BODY,{"derivedFrom":makeQuery(id+"F2.opPattern","COPY",BODY,{"derivedFrom":makeQuery(id+"F1.opRevolve","SWEPT_BODY",BODY,{"disambiguationData":[OSD([sQuery(id+"F0.wireOp",EDGE,"E1")])]}),"instanceName":"1"}),"instanceName":"1"}),"instanceName":"1"}),"instanceName":"1"}),"instanceName":"1"}),"instanceName":"1"});
            var Q677;
            Q677=makeQuery(id+"F11.opPattern","COPY",BODY,{"derivedFrom":makeQuery(id+"F10.opPattern","COPY",BODY,{"derivedFrom":makeQuery(id+"F9.opPattern","COPY",BODY,{"derivedFrom":makeQuery(id+"F5.opPattern","COPY",BODY,{"derivedFrom":makeQuery(id+"F1.opRevolve","SWEPT_BODY",BODY,{"disambiguationData":[OSD([sQuery(id+"F0.wireOp",EDGE,"E1")])]}),"instanceName":"1"}),"instanceName":"1"}),"instanceName":"1"}),"instanceName":"1"});
            var Q678;
            Q678=makeQuery(id+"F11.opPattern","COPY",BODY,{"derivedFrom":makeQuery(id+"F10.opPattern","COPY",BODY,{"derivedFrom":makeQuery(id+"F9.opPattern","COPY",BODY,{"derivedFrom":makeQuery(id+"F5.opPattern","COPY",BODY,{"derivedFrom":makeQuery(id+"F2.opPattern","COPY",BODY,{"derivedFrom":makeQuery(id+"F1.opRevolve","SWEPT_BODY",BODY,{"disambiguationData":[OSD([sQuery(id+"F0.wireOp",EDGE,"E1")])]}),"instanceName":"1"}),"instanceName":"1"}),"instanceName":"1"}),"instanceName":"1"}),"instanceName":"1"});
            var Q679;
            Q679=makeQuery(id+"F11.opPattern","COPY",BODY,{"derivedFrom":makeQuery(id+"F10.opPattern","COPY",BODY,{"derivedFrom":makeQuery(id+"F9.opPattern","COPY",BODY,{"derivedFrom":makeQuery(id+"F5.opPattern","COPY",BODY,{"derivedFrom":makeQuery(id+"F3.opPattern","COPY",BODY,{"derivedFrom":makeQuery(id+"F2.opPattern","COPY",BODY,{"derivedFrom":makeQuery(id+"F1.opRevolve","SWEPT_BODY",BODY,{"disambiguationData":[OSD([sQuery(id+"F0.wireOp",EDGE,"E1")])]}),"instanceName":"1"}),"instanceName":"1"}),"instanceName":"1"}),"instanceName":"1"}),"instanceName":"1"}),"instanceName":"1"});
            var Q680;
            Q680=makeQuery(id+"F11.opPattern","COPY",BODY,{"derivedFrom":makeQuery(id+"F10.opPattern","COPY",BODY,{"derivedFrom":makeQuery(id+"F9.opPattern","COPY",BODY,{"derivedFrom":makeQuery(id+"F5.opPattern","COPY",BODY,{"derivedFrom":makeQuery(id+"F4.opPattern","COPY",BODY,{"derivedFrom":makeQuery(id+"F1.opRevolve","SWEPT_BODY",BODY,{"disambiguationData":[OSD([sQuery(id+"F0.wireOp",EDGE,"E1")])]}),"instanceName":"1"}),"instanceName":"1"}),"instanceName":"1"}),"instanceName":"1"}),"instanceName":"1"});
            var Q681;
            Q681=makeQuery(id+"F11.opPattern","COPY",BODY,{"derivedFrom":makeQuery(id+"F10.opPattern","COPY",BODY,{"derivedFrom":makeQuery(id+"F9.opPattern","COPY",BODY,{"derivedFrom":makeQuery(id+"F5.opPattern","COPY",BODY,{"derivedFrom":makeQuery(id+"F4.opPattern","COPY",BODY,{"derivedFrom":makeQuery(id+"F2.opPattern","COPY",BODY,{"derivedFrom":makeQuery(id+"F1.opRevolve","SWEPT_BODY",BODY,{"disambiguationData":[OSD([sQuery(id+"F0.wireOp",EDGE,"E1")])]}),"instanceName":"1"}),"instanceName":"1"}),"instanceName":"1"}),"instanceName":"1"}),"instanceName":"1"}),"instanceName":"1"});
            var Q682;
            Q682=makeQuery(id+"F11.opPattern","COPY",BODY,{"derivedFrom":makeQuery(id+"F10.opPattern","COPY",BODY,{"derivedFrom":makeQuery(id+"F9.opPattern","COPY",BODY,{"derivedFrom":makeQuery(id+"F5.opPattern","COPY",BODY,{"derivedFrom":makeQuery(id+"F4.opPattern","COPY",BODY,{"derivedFrom":makeQuery(id+"F3.opPattern","COPY",BODY,{"derivedFrom":makeQuery(id+"F2.opPattern","COPY",BODY,{"derivedFrom":makeQuery(id+"F1.opRevolve","SWEPT_BODY",BODY,{"disambiguationData":[OSD([sQuery(id+"F0.wireOp",EDGE,"E1")])]}),"instanceName":"1"}),"instanceName":"1"}),"instanceName":"1"}),"instanceName":"1"}),"instanceName":"1"}),"instanceName":"1"}),"instanceName":"1"});
            var Q683;
            Q683=makeQuery(id+"F11.opPattern","COPY",BODY,{"derivedFrom":makeQuery(id+"F10.opPattern","COPY",BODY,{"derivedFrom":makeQuery(id+"F9.opPattern","COPY",BODY,{"derivedFrom":makeQuery(id+"F6.opPattern","COPY",BODY,{"derivedFrom":makeQuery(id+"F1.opRevolve","SWEPT_BODY",BODY,{"disambiguationData":[OSD([sQuery(id+"F0.wireOp",EDGE,"E1")])]}),"instanceName":"1"}),"instanceName":"1"}),"instanceName":"1"}),"instanceName":"1"});
            var Q684;
            Q684=makeQuery(id+"F11.opPattern","COPY",BODY,{"derivedFrom":makeQuery(id+"F10.opPattern","COPY",BODY,{"derivedFrom":makeQuery(id+"F9.opPattern","COPY",BODY,{"derivedFrom":makeQuery(id+"F6.opPattern","COPY",BODY,{"derivedFrom":makeQuery(id+"F2.opPattern","COPY",BODY,{"derivedFrom":makeQuery(id+"F1.opRevolve","SWEPT_BODY",BODY,{"disambiguationData":[OSD([sQuery(id+"F0.wireOp",EDGE,"E1")])]}),"instanceName":"1"}),"instanceName":"1"}),"instanceName":"1"}),"instanceName":"1"}),"instanceName":"1"});
            var Q685;
            Q685=makeQuery(id+"F11.opPattern","COPY",BODY,{"derivedFrom":makeQuery(id+"F10.opPattern","COPY",BODY,{"derivedFrom":makeQuery(id+"F9.opPattern","COPY",BODY,{"derivedFrom":makeQuery(id+"F6.opPattern","COPY",BODY,{"derivedFrom":makeQuery(id+"F3.opPattern","COPY",BODY,{"derivedFrom":makeQuery(id+"F2.opPattern","COPY",BODY,{"derivedFrom":makeQuery(id+"F1.opRevolve","SWEPT_BODY",BODY,{"disambiguationData":[OSD([sQuery(id+"F0.wireOp",EDGE,"E1")])]}),"instanceName":"1"}),"instanceName":"1"}),"instanceName":"1"}),"instanceName":"1"}),"instanceName":"1"}),"instanceName":"1"});
            var Q686;
            Q686=makeQuery(id+"F11.opPattern","COPY",BODY,{"derivedFrom":makeQuery(id+"F10.opPattern","COPY",BODY,{"derivedFrom":makeQuery(id+"F9.opPattern","COPY",BODY,{"derivedFrom":makeQuery(id+"F6.opPattern","COPY",BODY,{"derivedFrom":makeQuery(id+"F4.opPattern","COPY",BODY,{"derivedFrom":makeQuery(id+"F1.opRevolve","SWEPT_BODY",BODY,{"disambiguationData":[OSD([sQuery(id+"F0.wireOp",EDGE,"E1")])]}),"instanceName":"1"}),"instanceName":"1"}),"instanceName":"1"}),"instanceName":"1"}),"instanceName":"1"});
            var Q687;
            Q687=makeQuery(id+"F11.opPattern","COPY",BODY,{"derivedFrom":makeQuery(id+"F10.opPattern","COPY",BODY,{"derivedFrom":makeQuery(id+"F9.opPattern","COPY",BODY,{"derivedFrom":makeQuery(id+"F6.opPattern","COPY",BODY,{"derivedFrom":makeQuery(id+"F4.opPattern","COPY",BODY,{"derivedFrom":makeQuery(id+"F2.opPattern","COPY",BODY,{"derivedFrom":makeQuery(id+"F1.opRevolve","SWEPT_BODY",BODY,{"disambiguationData":[OSD([sQuery(id+"F0.wireOp",EDGE,"E1")])]}),"instanceName":"1"}),"instanceName":"1"}),"instanceName":"1"}),"instanceName":"1"}),"instanceName":"1"}),"instanceName":"1"});
            var Q688;
            Q688=makeQuery(id+"F11.opPattern","COPY",BODY,{"derivedFrom":makeQuery(id+"F10.opPattern","COPY",BODY,{"derivedFrom":makeQuery(id+"F9.opPattern","COPY",BODY,{"derivedFrom":makeQuery(id+"F6.opPattern","COPY",BODY,{"derivedFrom":makeQuery(id+"F4.opPattern","COPY",BODY,{"derivedFrom":makeQuery(id+"F3.opPattern","COPY",BODY,{"derivedFrom":makeQuery(id+"F2.opPattern","COPY",BODY,{"derivedFrom":makeQuery(id+"F1.opRevolve","SWEPT_BODY",BODY,{"disambiguationData":[OSD([sQuery(id+"F0.wireOp",EDGE,"E1")])]}),"instanceName":"1"}),"instanceName":"1"}),"instanceName":"1"}),"instanceName":"1"}),"instanceName":"1"}),"instanceName":"1"}),"instanceName":"1"});
            var Q689;
            Q689=makeQuery(id+"F11.opPattern","COPY",BODY,{"derivedFrom":makeQuery(id+"F10.opPattern","COPY",BODY,{"derivedFrom":makeQuery(id+"F9.opPattern","COPY",BODY,{"derivedFrom":makeQuery(id+"F6.opPattern","COPY",BODY,{"derivedFrom":makeQuery(id+"F5.opPattern","COPY",BODY,{"derivedFrom":makeQuery(id+"F1.opRevolve","SWEPT_BODY",BODY,{"disambiguationData":[OSD([sQuery(id+"F0.wireOp",EDGE,"E1")])]}),"instanceName":"1"}),"instanceName":"1"}),"instanceName":"1"}),"instanceName":"1"}),"instanceName":"1"});
            var Q690;
            Q690=makeQuery(id+"F11.opPattern","COPY",BODY,{"derivedFrom":makeQuery(id+"F10.opPattern","COPY",BODY,{"derivedFrom":makeQuery(id+"F9.opPattern","COPY",BODY,{"derivedFrom":makeQuery(id+"F6.opPattern","COPY",BODY,{"derivedFrom":makeQuery(id+"F5.opPattern","COPY",BODY,{"derivedFrom":makeQuery(id+"F2.opPattern","COPY",BODY,{"derivedFrom":makeQuery(id+"F1.opRevolve","SWEPT_BODY",BODY,{"disambiguationData":[OSD([sQuery(id+"F0.wireOp",EDGE,"E1")])]}),"instanceName":"1"}),"instanceName":"1"}),"instanceName":"1"}),"instanceName":"1"}),"instanceName":"1"}),"instanceName":"1"});
            var Q691;
            Q691=makeQuery(id+"F11.opPattern","COPY",BODY,{"derivedFrom":makeQuery(id+"F10.opPattern","COPY",BODY,{"derivedFrom":makeQuery(id+"F9.opPattern","COPY",BODY,{"derivedFrom":makeQuery(id+"F6.opPattern","COPY",BODY,{"derivedFrom":makeQuery(id+"F5.opPattern","COPY",BODY,{"derivedFrom":makeQuery(id+"F3.opPattern","COPY",BODY,{"derivedFrom":makeQuery(id+"F2.opPattern","COPY",BODY,{"derivedFrom":makeQuery(id+"F1.opRevolve","SWEPT_BODY",BODY,{"disambiguationData":[OSD([sQuery(id+"F0.wireOp",EDGE,"E1")])]}),"instanceName":"1"}),"instanceName":"1"}),"instanceName":"1"}),"instanceName":"1"}),"instanceName":"1"}),"instanceName":"1"}),"instanceName":"1"});
            var Q692;
            Q692=makeQuery(id+"F11.opPattern","COPY",BODY,{"derivedFrom":makeQuery(id+"F10.opPattern","COPY",BODY,{"derivedFrom":makeQuery(id+"F9.opPattern","COPY",BODY,{"derivedFrom":makeQuery(id+"F6.opPattern","COPY",BODY,{"derivedFrom":makeQuery(id+"F5.opPattern","COPY",BODY,{"derivedFrom":makeQuery(id+"F4.opPattern","COPY",BODY,{"derivedFrom":makeQuery(id+"F1.opRevolve","SWEPT_BODY",BODY,{"disambiguationData":[OSD([sQuery(id+"F0.wireOp",EDGE,"E1")])]}),"instanceName":"1"}),"instanceName":"1"}),"instanceName":"1"}),"instanceName":"1"}),"instanceName":"1"}),"instanceName":"1"});
            var Q693;
            Q693=makeQuery(id+"F11.opPattern","COPY",BODY,{"derivedFrom":makeQuery(id+"F10.opPattern","COPY",BODY,{"derivedFrom":makeQuery(id+"F9.opPattern","COPY",BODY,{"derivedFrom":makeQuery(id+"F6.opPattern","COPY",BODY,{"derivedFrom":makeQuery(id+"F5.opPattern","COPY",BODY,{"derivedFrom":makeQuery(id+"F4.opPattern","COPY",BODY,{"derivedFrom":makeQuery(id+"F2.opPattern","COPY",BODY,{"derivedFrom":makeQuery(id+"F1.opRevolve","SWEPT_BODY",BODY,{"disambiguationData":[OSD([sQuery(id+"F0.wireOp",EDGE,"E1")])]}),"instanceName":"1"}),"instanceName":"1"}),"instanceName":"1"}),"instanceName":"1"}),"instanceName":"1"}),"instanceName":"1"}),"instanceName":"1"});
            var Q694;
            Q694=makeQuery(id+"F11.opPattern","COPY",BODY,{"derivedFrom":makeQuery(id+"F10.opPattern","COPY",BODY,{"derivedFrom":makeQuery(id+"F9.opPattern","COPY",BODY,{"derivedFrom":makeQuery(id+"F6.opPattern","COPY",BODY,{"derivedFrom":makeQuery(id+"F5.opPattern","COPY",BODY,{"derivedFrom":makeQuery(id+"F4.opPattern","COPY",BODY,{"derivedFrom":makeQuery(id+"F3.opPattern","COPY",BODY,{"derivedFrom":makeQuery(id+"F2.opPattern","COPY",BODY,{"derivedFrom":makeQuery(id+"F1.opRevolve","SWEPT_BODY",BODY,{"disambiguationData":[OSD([sQuery(id+"F0.wireOp",EDGE,"E1")])]}),"instanceName":"1"}),"instanceName":"1"}),"instanceName":"1"}),"instanceName":"1"}),"instanceName":"1"}),"instanceName":"1"}),"instanceName":"1"}),"instanceName":"1"});
            var Q695;
            Q695=makeQuery(id+"F11.opPattern","COPY",BODY,{"derivedFrom":makeQuery(id+"F10.opPattern","COPY",BODY,{"derivedFrom":makeQuery(id+"F9.opPattern","COPY",BODY,{"derivedFrom":makeQuery(id+"F7.opPattern","COPY",BODY,{"derivedFrom":makeQuery(id+"F1.opRevolve","SWEPT_BODY",BODY,{"disambiguationData":[OSD([sQuery(id+"F0.wireOp",EDGE,"E1")])]}),"instanceName":"1"}),"instanceName":"1"}),"instanceName":"1"}),"instanceName":"1"});
            var Q696;
            Q696=makeQuery(id+"F11.opPattern","COPY",BODY,{"derivedFrom":makeQuery(id+"F10.opPattern","COPY",BODY,{"derivedFrom":makeQuery(id+"F9.opPattern","COPY",BODY,{"derivedFrom":makeQuery(id+"F7.opPattern","COPY",BODY,{"derivedFrom":makeQuery(id+"F2.opPattern","COPY",BODY,{"derivedFrom":makeQuery(id+"F1.opRevolve","SWEPT_BODY",BODY,{"disambiguationData":[OSD([sQuery(id+"F0.wireOp",EDGE,"E1")])]}),"instanceName":"1"}),"instanceName":"1"}),"instanceName":"1"}),"instanceName":"1"}),"instanceName":"1"});
            var Q697;
            Q697=makeQuery(id+"F11.opPattern","COPY",BODY,{"derivedFrom":makeQuery(id+"F10.opPattern","COPY",BODY,{"derivedFrom":makeQuery(id+"F9.opPattern","COPY",BODY,{"derivedFrom":makeQuery(id+"F7.opPattern","COPY",BODY,{"derivedFrom":makeQuery(id+"F3.opPattern","COPY",BODY,{"derivedFrom":makeQuery(id+"F2.opPattern","COPY",BODY,{"derivedFrom":makeQuery(id+"F1.opRevolve","SWEPT_BODY",BODY,{"disambiguationData":[OSD([sQuery(id+"F0.wireOp",EDGE,"E1")])]}),"instanceName":"1"}),"instanceName":"1"}),"instanceName":"1"}),"instanceName":"1"}),"instanceName":"1"}),"instanceName":"1"});
            var Q698;
            Q698=makeQuery(id+"F11.opPattern","COPY",BODY,{"derivedFrom":makeQuery(id+"F10.opPattern","COPY",BODY,{"derivedFrom":makeQuery(id+"F9.opPattern","COPY",BODY,{"derivedFrom":makeQuery(id+"F7.opPattern","COPY",BODY,{"derivedFrom":makeQuery(id+"F4.opPattern","COPY",BODY,{"derivedFrom":makeQuery(id+"F1.opRevolve","SWEPT_BODY",BODY,{"disambiguationData":[OSD([sQuery(id+"F0.wireOp",EDGE,"E1")])]}),"instanceName":"1"}),"instanceName":"1"}),"instanceName":"1"}),"instanceName":"1"}),"instanceName":"1"});
            var Q699;
            Q699=makeQuery(id+"F11.opPattern","COPY",BODY,{"derivedFrom":makeQuery(id+"F10.opPattern","COPY",BODY,{"derivedFrom":makeQuery(id+"F9.opPattern","COPY",BODY,{"derivedFrom":makeQuery(id+"F7.opPattern","COPY",BODY,{"derivedFrom":makeQuery(id+"F4.opPattern","COPY",BODY,{"derivedFrom":makeQuery(id+"F2.opPattern","COPY",BODY,{"derivedFrom":makeQuery(id+"F1.opRevolve","SWEPT_BODY",BODY,{"disambiguationData":[OSD([sQuery(id+"F0.wireOp",EDGE,"E1")])]}),"instanceName":"1"}),"instanceName":"1"}),"instanceName":"1"}),"instanceName":"1"}),"instanceName":"1"}),"instanceName":"1"});
            var Q700;
            Q700=makeQuery(id+"F11.opPattern","COPY",BODY,{"derivedFrom":makeQuery(id+"F10.opPattern","COPY",BODY,{"derivedFrom":makeQuery(id+"F9.opPattern","COPY",BODY,{"derivedFrom":makeQuery(id+"F7.opPattern","COPY",BODY,{"derivedFrom":makeQuery(id+"F4.opPattern","COPY",BODY,{"derivedFrom":makeQuery(id+"F3.opPattern","COPY",BODY,{"derivedFrom":makeQuery(id+"F2.opPattern","COPY",BODY,{"derivedFrom":makeQuery(id+"F1.opRevolve","SWEPT_BODY",BODY,{"disambiguationData":[OSD([sQuery(id+"F0.wireOp",EDGE,"E1")])]}),"instanceName":"1"}),"instanceName":"1"}),"instanceName":"1"}),"instanceName":"1"}),"instanceName":"1"}),"instanceName":"1"}),"instanceName":"1"});
            var Q701;
            Q701=makeQuery(id+"F11.opPattern","COPY",BODY,{"derivedFrom":makeQuery(id+"F10.opPattern","COPY",BODY,{"derivedFrom":makeQuery(id+"F9.opPattern","COPY",BODY,{"derivedFrom":makeQuery(id+"F7.opPattern","COPY",BODY,{"derivedFrom":makeQuery(id+"F5.opPattern","COPY",BODY,{"derivedFrom":makeQuery(id+"F1.opRevolve","SWEPT_BODY",BODY,{"disambiguationData":[OSD([sQuery(id+"F0.wireOp",EDGE,"E1")])]}),"instanceName":"1"}),"instanceName":"1"}),"instanceName":"1"}),"instanceName":"1"}),"instanceName":"1"});
            var Q702;
            Q702=makeQuery(id+"F11.opPattern","COPY",BODY,{"derivedFrom":makeQuery(id+"F10.opPattern","COPY",BODY,{"derivedFrom":makeQuery(id+"F9.opPattern","COPY",BODY,{"derivedFrom":makeQuery(id+"F7.opPattern","COPY",BODY,{"derivedFrom":makeQuery(id+"F5.opPattern","COPY",BODY,{"derivedFrom":makeQuery(id+"F2.opPattern","COPY",BODY,{"derivedFrom":makeQuery(id+"F1.opRevolve","SWEPT_BODY",BODY,{"disambiguationData":[OSD([sQuery(id+"F0.wireOp",EDGE,"E1")])]}),"instanceName":"1"}),"instanceName":"1"}),"instanceName":"1"}),"instanceName":"1"}),"instanceName":"1"}),"instanceName":"1"});
            var Q703;
            Q703=makeQuery(id+"F11.opPattern","COPY",BODY,{"derivedFrom":makeQuery(id+"F10.opPattern","COPY",BODY,{"derivedFrom":makeQuery(id+"F9.opPattern","COPY",BODY,{"derivedFrom":makeQuery(id+"F7.opPattern","COPY",BODY,{"derivedFrom":makeQuery(id+"F5.opPattern","COPY",BODY,{"derivedFrom":makeQuery(id+"F3.opPattern","COPY",BODY,{"derivedFrom":makeQuery(id+"F2.opPattern","COPY",BODY,{"derivedFrom":makeQuery(id+"F1.opRevolve","SWEPT_BODY",BODY,{"disambiguationData":[OSD([sQuery(id+"F0.wireOp",EDGE,"E1")])]}),"instanceName":"1"}),"instanceName":"1"}),"instanceName":"1"}),"instanceName":"1"}),"instanceName":"1"}),"instanceName":"1"}),"instanceName":"1"});
            var Q704;
            Q704=makeQuery(id+"F11.opPattern","COPY",BODY,{"derivedFrom":makeQuery(id+"F10.opPattern","COPY",BODY,{"derivedFrom":makeQuery(id+"F9.opPattern","COPY",BODY,{"derivedFrom":makeQuery(id+"F7.opPattern","COPY",BODY,{"derivedFrom":makeQuery(id+"F5.opPattern","COPY",BODY,{"derivedFrom":makeQuery(id+"F4.opPattern","COPY",BODY,{"derivedFrom":makeQuery(id+"F1.opRevolve","SWEPT_BODY",BODY,{"disambiguationData":[OSD([sQuery(id+"F0.wireOp",EDGE,"E1")])]}),"instanceName":"1"}),"instanceName":"1"}),"instanceName":"1"}),"instanceName":"1"}),"instanceName":"1"}),"instanceName":"1"});
            var Q705;
            Q705=makeQuery(id+"F11.opPattern","COPY",BODY,{"derivedFrom":makeQuery(id+"F10.opPattern","COPY",BODY,{"derivedFrom":makeQuery(id+"F9.opPattern","COPY",BODY,{"derivedFrom":makeQuery(id+"F7.opPattern","COPY",BODY,{"derivedFrom":makeQuery(id+"F5.opPattern","COPY",BODY,{"derivedFrom":makeQuery(id+"F4.opPattern","COPY",BODY,{"derivedFrom":makeQuery(id+"F2.opPattern","COPY",BODY,{"derivedFrom":makeQuery(id+"F1.opRevolve","SWEPT_BODY",BODY,{"disambiguationData":[OSD([sQuery(id+"F0.wireOp",EDGE,"E1")])]}),"instanceName":"1"}),"instanceName":"1"}),"instanceName":"1"}),"instanceName":"1"}),"instanceName":"1"}),"instanceName":"1"}),"instanceName":"1"});
            var Q706;
            Q706=makeQuery(id+"F11.opPattern","COPY",BODY,{"derivedFrom":makeQuery(id+"F10.opPattern","COPY",BODY,{"derivedFrom":makeQuery(id+"F9.opPattern","COPY",BODY,{"derivedFrom":makeQuery(id+"F7.opPattern","COPY",BODY,{"derivedFrom":makeQuery(id+"F5.opPattern","COPY",BODY,{"derivedFrom":makeQuery(id+"F4.opPattern","COPY",BODY,{"derivedFrom":makeQuery(id+"F3.opPattern","COPY",BODY,{"derivedFrom":makeQuery(id+"F2.opPattern","COPY",BODY,{"derivedFrom":makeQuery(id+"F1.opRevolve","SWEPT_BODY",BODY,{"disambiguationData":[OSD([sQuery(id+"F0.wireOp",EDGE,"E1")])]}),"instanceName":"1"}),"instanceName":"1"}),"instanceName":"1"}),"instanceName":"1"}),"instanceName":"1"}),"instanceName":"1"}),"instanceName":"1"}),"instanceName":"1"});
            var Q707;
            Q707=makeQuery(id+"F11.opPattern","COPY",BODY,{"derivedFrom":makeQuery(id+"F10.opPattern","COPY",BODY,{"derivedFrom":makeQuery(id+"F9.opPattern","COPY",BODY,{"derivedFrom":makeQuery(id+"F7.opPattern","COPY",BODY,{"derivedFrom":makeQuery(id+"F6.opPattern","COPY",BODY,{"derivedFrom":makeQuery(id+"F1.opRevolve","SWEPT_BODY",BODY,{"disambiguationData":[OSD([sQuery(id+"F0.wireOp",EDGE,"E1")])]}),"instanceName":"1"}),"instanceName":"1"}),"instanceName":"1"}),"instanceName":"1"}),"instanceName":"1"});
            var Q708;
            Q708=makeQuery(id+"F11.opPattern","COPY",BODY,{"derivedFrom":makeQuery(id+"F10.opPattern","COPY",BODY,{"derivedFrom":makeQuery(id+"F9.opPattern","COPY",BODY,{"derivedFrom":makeQuery(id+"F7.opPattern","COPY",BODY,{"derivedFrom":makeQuery(id+"F6.opPattern","COPY",BODY,{"derivedFrom":makeQuery(id+"F2.opPattern","COPY",BODY,{"derivedFrom":makeQuery(id+"F1.opRevolve","SWEPT_BODY",BODY,{"disambiguationData":[OSD([sQuery(id+"F0.wireOp",EDGE,"E1")])]}),"instanceName":"1"}),"instanceName":"1"}),"instanceName":"1"}),"instanceName":"1"}),"instanceName":"1"}),"instanceName":"1"});
            var Q709;
            Q709=makeQuery(id+"F11.opPattern","COPY",BODY,{"derivedFrom":makeQuery(id+"F10.opPattern","COPY",BODY,{"derivedFrom":makeQuery(id+"F9.opPattern","COPY",BODY,{"derivedFrom":makeQuery(id+"F7.opPattern","COPY",BODY,{"derivedFrom":makeQuery(id+"F6.opPattern","COPY",BODY,{"derivedFrom":makeQuery(id+"F3.opPattern","COPY",BODY,{"derivedFrom":makeQuery(id+"F2.opPattern","COPY",BODY,{"derivedFrom":makeQuery(id+"F1.opRevolve","SWEPT_BODY",BODY,{"disambiguationData":[OSD([sQuery(id+"F0.wireOp",EDGE,"E1")])]}),"instanceName":"1"}),"instanceName":"1"}),"instanceName":"1"}),"instanceName":"1"}),"instanceName":"1"}),"instanceName":"1"}),"instanceName":"1"});
            var Q710;
            Q710=makeQuery(id+"F11.opPattern","COPY",BODY,{"derivedFrom":makeQuery(id+"F10.opPattern","COPY",BODY,{"derivedFrom":makeQuery(id+"F9.opPattern","COPY",BODY,{"derivedFrom":makeQuery(id+"F7.opPattern","COPY",BODY,{"derivedFrom":makeQuery(id+"F6.opPattern","COPY",BODY,{"derivedFrom":makeQuery(id+"F4.opPattern","COPY",BODY,{"derivedFrom":makeQuery(id+"F1.opRevolve","SWEPT_BODY",BODY,{"disambiguationData":[OSD([sQuery(id+"F0.wireOp",EDGE,"E1")])]}),"instanceName":"1"}),"instanceName":"1"}),"instanceName":"1"}),"instanceName":"1"}),"instanceName":"1"}),"instanceName":"1"});
            var Q711;
            Q711=makeQuery(id+"F11.opPattern","COPY",BODY,{"derivedFrom":makeQuery(id+"F10.opPattern","COPY",BODY,{"derivedFrom":makeQuery(id+"F9.opPattern","COPY",BODY,{"derivedFrom":makeQuery(id+"F7.opPattern","COPY",BODY,{"derivedFrom":makeQuery(id+"F6.opPattern","COPY",BODY,{"derivedFrom":makeQuery(id+"F4.opPattern","COPY",BODY,{"derivedFrom":makeQuery(id+"F2.opPattern","COPY",BODY,{"derivedFrom":makeQuery(id+"F1.opRevolve","SWEPT_BODY",BODY,{"disambiguationData":[OSD([sQuery(id+"F0.wireOp",EDGE,"E1")])]}),"instanceName":"1"}),"instanceName":"1"}),"instanceName":"1"}),"instanceName":"1"}),"instanceName":"1"}),"instanceName":"1"}),"instanceName":"1"});
            var Q712;
            Q712=makeQuery(id+"F11.opPattern","COPY",BODY,{"derivedFrom":makeQuery(id+"F10.opPattern","COPY",BODY,{"derivedFrom":makeQuery(id+"F9.opPattern","COPY",BODY,{"derivedFrom":makeQuery(id+"F7.opPattern","COPY",BODY,{"derivedFrom":makeQuery(id+"F6.opPattern","COPY",BODY,{"derivedFrom":makeQuery(id+"F4.opPattern","COPY",BODY,{"derivedFrom":makeQuery(id+"F3.opPattern","COPY",BODY,{"derivedFrom":makeQuery(id+"F2.opPattern","COPY",BODY,{"derivedFrom":makeQuery(id+"F1.opRevolve","SWEPT_BODY",BODY,{"disambiguationData":[OSD([sQuery(id+"F0.wireOp",EDGE,"E1")])]}),"instanceName":"1"}),"instanceName":"1"}),"instanceName":"1"}),"instanceName":"1"}),"instanceName":"1"}),"instanceName":"1"}),"instanceName":"1"}),"instanceName":"1"});
            var Q713;
            Q713=makeQuery(id+"F11.opPattern","COPY",BODY,{"derivedFrom":makeQuery(id+"F10.opPattern","COPY",BODY,{"derivedFrom":makeQuery(id+"F9.opPattern","COPY",BODY,{"derivedFrom":makeQuery(id+"F7.opPattern","COPY",BODY,{"derivedFrom":makeQuery(id+"F6.opPattern","COPY",BODY,{"derivedFrom":makeQuery(id+"F5.opPattern","COPY",BODY,{"derivedFrom":makeQuery(id+"F1.opRevolve","SWEPT_BODY",BODY,{"disambiguationData":[OSD([sQuery(id+"F0.wireOp",EDGE,"E1")])]}),"instanceName":"1"}),"instanceName":"1"}),"instanceName":"1"}),"instanceName":"1"}),"instanceName":"1"}),"instanceName":"1"});
            var Q714;
            Q714=makeQuery(id+"F11.opPattern","COPY",BODY,{"derivedFrom":makeQuery(id+"F10.opPattern","COPY",BODY,{"derivedFrom":makeQuery(id+"F9.opPattern","COPY",BODY,{"derivedFrom":makeQuery(id+"F7.opPattern","COPY",BODY,{"derivedFrom":makeQuery(id+"F6.opPattern","COPY",BODY,{"derivedFrom":makeQuery(id+"F5.opPattern","COPY",BODY,{"derivedFrom":makeQuery(id+"F2.opPattern","COPY",BODY,{"derivedFrom":makeQuery(id+"F1.opRevolve","SWEPT_BODY",BODY,{"disambiguationData":[OSD([sQuery(id+"F0.wireOp",EDGE,"E1")])]}),"instanceName":"1"}),"instanceName":"1"}),"instanceName":"1"}),"instanceName":"1"}),"instanceName":"1"}),"instanceName":"1"}),"instanceName":"1"});
            var Q715;
            Q715=makeQuery(id+"F11.opPattern","COPY",BODY,{"derivedFrom":makeQuery(id+"F10.opPattern","COPY",BODY,{"derivedFrom":makeQuery(id+"F9.opPattern","COPY",BODY,{"derivedFrom":makeQuery(id+"F7.opPattern","COPY",BODY,{"derivedFrom":makeQuery(id+"F6.opPattern","COPY",BODY,{"derivedFrom":makeQuery(id+"F5.opPattern","COPY",BODY,{"derivedFrom":makeQuery(id+"F3.opPattern","COPY",BODY,{"derivedFrom":makeQuery(id+"F2.opPattern","COPY",BODY,{"derivedFrom":makeQuery(id+"F1.opRevolve","SWEPT_BODY",BODY,{"disambiguationData":[OSD([sQuery(id+"F0.wireOp",EDGE,"E1")])]}),"instanceName":"1"}),"instanceName":"1"}),"instanceName":"1"}),"instanceName":"1"}),"instanceName":"1"}),"instanceName":"1"}),"instanceName":"1"}),"instanceName":"1"});
            var Q716;
            Q716=makeQuery(id+"F11.opPattern","COPY",BODY,{"derivedFrom":makeQuery(id+"F10.opPattern","COPY",BODY,{"derivedFrom":makeQuery(id+"F9.opPattern","COPY",BODY,{"derivedFrom":makeQuery(id+"F7.opPattern","COPY",BODY,{"derivedFrom":makeQuery(id+"F6.opPattern","COPY",BODY,{"derivedFrom":makeQuery(id+"F5.opPattern","COPY",BODY,{"derivedFrom":makeQuery(id+"F4.opPattern","COPY",BODY,{"derivedFrom":makeQuery(id+"F1.opRevolve","SWEPT_BODY",BODY,{"disambiguationData":[OSD([sQuery(id+"F0.wireOp",EDGE,"E1")])]}),"instanceName":"1"}),"instanceName":"1"}),"instanceName":"1"}),"instanceName":"1"}),"instanceName":"1"}),"instanceName":"1"}),"instanceName":"1"});
            var Q717;
            Q717=makeQuery(id+"F11.opPattern","COPY",BODY,{"derivedFrom":makeQuery(id+"F10.opPattern","COPY",BODY,{"derivedFrom":makeQuery(id+"F9.opPattern","COPY",BODY,{"derivedFrom":makeQuery(id+"F7.opPattern","COPY",BODY,{"derivedFrom":makeQuery(id+"F6.opPattern","COPY",BODY,{"derivedFrom":makeQuery(id+"F5.opPattern","COPY",BODY,{"derivedFrom":makeQuery(id+"F4.opPattern","COPY",BODY,{"derivedFrom":makeQuery(id+"F2.opPattern","COPY",BODY,{"derivedFrom":makeQuery(id+"F1.opRevolve","SWEPT_BODY",BODY,{"disambiguationData":[OSD([sQuery(id+"F0.wireOp",EDGE,"E1")])]}),"instanceName":"1"}),"instanceName":"1"}),"instanceName":"1"}),"instanceName":"1"}),"instanceName":"1"}),"instanceName":"1"}),"instanceName":"1"}),"instanceName":"1"});
            var Q718;
            Q718=makeQuery(id+"F11.opPattern","COPY",BODY,{"derivedFrom":makeQuery(id+"F10.opPattern","COPY",BODY,{"derivedFrom":makeQuery(id+"F9.opPattern","COPY",BODY,{"derivedFrom":makeQuery(id+"F7.opPattern","COPY",BODY,{"derivedFrom":makeQuery(id+"F6.opPattern","COPY",BODY,{"derivedFrom":makeQuery(id+"F5.opPattern","COPY",BODY,{"derivedFrom":makeQuery(id+"F4.opPattern","COPY",BODY,{"derivedFrom":makeQuery(id+"F3.opPattern","COPY",BODY,{"derivedFrom":makeQuery(id+"F2.opPattern","COPY",BODY,{"derivedFrom":makeQuery(id+"F1.opRevolve","SWEPT_BODY",BODY,{"disambiguationData":[OSD([sQuery(id+"F0.wireOp",EDGE,"E1")])]}),"instanceName":"1"}),"instanceName":"1"}),"instanceName":"1"}),"instanceName":"1"}),"instanceName":"1"}),"instanceName":"1"}),"instanceName":"1"}),"instanceName":"1"}),"instanceName":"1"});
            var Q719;
            Q719=makeQuery(id+"F11.opPattern","COPY",BODY,{"derivedFrom":makeQuery(id+"F10.opPattern","COPY",BODY,{"derivedFrom":makeQuery(id+"F9.opPattern","COPY",BODY,{"derivedFrom":makeQuery(id+"F8.opPattern","COPY",BODY,{"derivedFrom":makeQuery(id+"F1.opRevolve","SWEPT_BODY",BODY,{"disambiguationData":[OSD([sQuery(id+"F0.wireOp",EDGE,"E1")])]}),"instanceName":"1"}),"instanceName":"1"}),"instanceName":"1"}),"instanceName":"1"});
            var Q720;
            Q720=makeQuery(id+"F11.opPattern","COPY",BODY,{"derivedFrom":makeQuery(id+"F10.opPattern","COPY",BODY,{"derivedFrom":makeQuery(id+"F9.opPattern","COPY",BODY,{"derivedFrom":makeQuery(id+"F8.opPattern","COPY",BODY,{"derivedFrom":makeQuery(id+"F2.opPattern","COPY",BODY,{"derivedFrom":makeQuery(id+"F1.opRevolve","SWEPT_BODY",BODY,{"disambiguationData":[OSD([sQuery(id+"F0.wireOp",EDGE,"E1")])]}),"instanceName":"1"}),"instanceName":"1"}),"instanceName":"1"}),"instanceName":"1"}),"instanceName":"1"});
            var Q721;
            Q721=makeQuery(id+"F11.opPattern","COPY",BODY,{"derivedFrom":makeQuery(id+"F10.opPattern","COPY",BODY,{"derivedFrom":makeQuery(id+"F9.opPattern","COPY",BODY,{"derivedFrom":makeQuery(id+"F8.opPattern","COPY",BODY,{"derivedFrom":makeQuery(id+"F3.opPattern","COPY",BODY,{"derivedFrom":makeQuery(id+"F2.opPattern","COPY",BODY,{"derivedFrom":makeQuery(id+"F1.opRevolve","SWEPT_BODY",BODY,{"disambiguationData":[OSD([sQuery(id+"F0.wireOp",EDGE,"E1")])]}),"instanceName":"1"}),"instanceName":"1"}),"instanceName":"1"}),"instanceName":"1"}),"instanceName":"1"}),"instanceName":"1"});
            var Q722;
            Q722=makeQuery(id+"F11.opPattern","COPY",BODY,{"derivedFrom":makeQuery(id+"F10.opPattern","COPY",BODY,{"derivedFrom":makeQuery(id+"F9.opPattern","COPY",BODY,{"derivedFrom":makeQuery(id+"F8.opPattern","COPY",BODY,{"derivedFrom":makeQuery(id+"F4.opPattern","COPY",BODY,{"derivedFrom":makeQuery(id+"F1.opRevolve","SWEPT_BODY",BODY,{"disambiguationData":[OSD([sQuery(id+"F0.wireOp",EDGE,"E1")])]}),"instanceName":"1"}),"instanceName":"1"}),"instanceName":"1"}),"instanceName":"1"}),"instanceName":"1"});
            var Q723;
            Q723=makeQuery(id+"F11.opPattern","COPY",BODY,{"derivedFrom":makeQuery(id+"F10.opPattern","COPY",BODY,{"derivedFrom":makeQuery(id+"F9.opPattern","COPY",BODY,{"derivedFrom":makeQuery(id+"F8.opPattern","COPY",BODY,{"derivedFrom":makeQuery(id+"F4.opPattern","COPY",BODY,{"derivedFrom":makeQuery(id+"F2.opPattern","COPY",BODY,{"derivedFrom":makeQuery(id+"F1.opRevolve","SWEPT_BODY",BODY,{"disambiguationData":[OSD([sQuery(id+"F0.wireOp",EDGE,"E1")])]}),"instanceName":"1"}),"instanceName":"1"}),"instanceName":"1"}),"instanceName":"1"}),"instanceName":"1"}),"instanceName":"1"});
            var Q724;
            Q724=makeQuery(id+"F11.opPattern","COPY",BODY,{"derivedFrom":makeQuery(id+"F10.opPattern","COPY",BODY,{"derivedFrom":makeQuery(id+"F9.opPattern","COPY",BODY,{"derivedFrom":makeQuery(id+"F8.opPattern","COPY",BODY,{"derivedFrom":makeQuery(id+"F4.opPattern","COPY",BODY,{"derivedFrom":makeQuery(id+"F3.opPattern","COPY",BODY,{"derivedFrom":makeQuery(id+"F2.opPattern","COPY",BODY,{"derivedFrom":makeQuery(id+"F1.opRevolve","SWEPT_BODY",BODY,{"disambiguationData":[OSD([sQuery(id+"F0.wireOp",EDGE,"E1")])]}),"instanceName":"1"}),"instanceName":"1"}),"instanceName":"1"}),"instanceName":"1"}),"instanceName":"1"}),"instanceName":"1"}),"instanceName":"1"});
            var Q725;
            Q725=makeQuery(id+"F11.opPattern","COPY",BODY,{"derivedFrom":makeQuery(id+"F10.opPattern","COPY",BODY,{"derivedFrom":makeQuery(id+"F9.opPattern","COPY",BODY,{"derivedFrom":makeQuery(id+"F8.opPattern","COPY",BODY,{"derivedFrom":makeQuery(id+"F5.opPattern","COPY",BODY,{"derivedFrom":makeQuery(id+"F1.opRevolve","SWEPT_BODY",BODY,{"disambiguationData":[OSD([sQuery(id+"F0.wireOp",EDGE,"E1")])]}),"instanceName":"1"}),"instanceName":"1"}),"instanceName":"1"}),"instanceName":"1"}),"instanceName":"1"});
            var Q726;
            Q726=makeQuery(id+"F11.opPattern","COPY",BODY,{"derivedFrom":makeQuery(id+"F10.opPattern","COPY",BODY,{"derivedFrom":makeQuery(id+"F9.opPattern","COPY",BODY,{"derivedFrom":makeQuery(id+"F8.opPattern","COPY",BODY,{"derivedFrom":makeQuery(id+"F5.opPattern","COPY",BODY,{"derivedFrom":makeQuery(id+"F2.opPattern","COPY",BODY,{"derivedFrom":makeQuery(id+"F1.opRevolve","SWEPT_BODY",BODY,{"disambiguationData":[OSD([sQuery(id+"F0.wireOp",EDGE,"E1")])]}),"instanceName":"1"}),"instanceName":"1"}),"instanceName":"1"}),"instanceName":"1"}),"instanceName":"1"}),"instanceName":"1"});
            var Q727;
            Q727=makeQuery(id+"F11.opPattern","COPY",BODY,{"derivedFrom":makeQuery(id+"F10.opPattern","COPY",BODY,{"derivedFrom":makeQuery(id+"F9.opPattern","COPY",BODY,{"derivedFrom":makeQuery(id+"F8.opPattern","COPY",BODY,{"derivedFrom":makeQuery(id+"F5.opPattern","COPY",BODY,{"derivedFrom":makeQuery(id+"F3.opPattern","COPY",BODY,{"derivedFrom":makeQuery(id+"F2.opPattern","COPY",BODY,{"derivedFrom":makeQuery(id+"F1.opRevolve","SWEPT_BODY",BODY,{"disambiguationData":[OSD([sQuery(id+"F0.wireOp",EDGE,"E1")])]}),"instanceName":"1"}),"instanceName":"1"}),"instanceName":"1"}),"instanceName":"1"}),"instanceName":"1"}),"instanceName":"1"}),"instanceName":"1"});
            var Q728;
            Q728=makeQuery(id+"F11.opPattern","COPY",BODY,{"derivedFrom":makeQuery(id+"F10.opPattern","COPY",BODY,{"derivedFrom":makeQuery(id+"F9.opPattern","COPY",BODY,{"derivedFrom":makeQuery(id+"F8.opPattern","COPY",BODY,{"derivedFrom":makeQuery(id+"F5.opPattern","COPY",BODY,{"derivedFrom":makeQuery(id+"F4.opPattern","COPY",BODY,{"derivedFrom":makeQuery(id+"F1.opRevolve","SWEPT_BODY",BODY,{"disambiguationData":[OSD([sQuery(id+"F0.wireOp",EDGE,"E1")])]}),"instanceName":"1"}),"instanceName":"1"}),"instanceName":"1"}),"instanceName":"1"}),"instanceName":"1"}),"instanceName":"1"});
            var Q729;
            Q729=makeQuery(id+"F11.opPattern","COPY",BODY,{"derivedFrom":makeQuery(id+"F10.opPattern","COPY",BODY,{"derivedFrom":makeQuery(id+"F9.opPattern","COPY",BODY,{"derivedFrom":makeQuery(id+"F8.opPattern","COPY",BODY,{"derivedFrom":makeQuery(id+"F5.opPattern","COPY",BODY,{"derivedFrom":makeQuery(id+"F4.opPattern","COPY",BODY,{"derivedFrom":makeQuery(id+"F2.opPattern","COPY",BODY,{"derivedFrom":makeQuery(id+"F1.opRevolve","SWEPT_BODY",BODY,{"disambiguationData":[OSD([sQuery(id+"F0.wireOp",EDGE,"E1")])]}),"instanceName":"1"}),"instanceName":"1"}),"instanceName":"1"}),"instanceName":"1"}),"instanceName":"1"}),"instanceName":"1"}),"instanceName":"1"});
            var Q730;
            Q730=makeQuery(id+"F11.opPattern","COPY",BODY,{"derivedFrom":makeQuery(id+"F10.opPattern","COPY",BODY,{"derivedFrom":makeQuery(id+"F9.opPattern","COPY",BODY,{"derivedFrom":makeQuery(id+"F8.opPattern","COPY",BODY,{"derivedFrom":makeQuery(id+"F5.opPattern","COPY",BODY,{"derivedFrom":makeQuery(id+"F4.opPattern","COPY",BODY,{"derivedFrom":makeQuery(id+"F3.opPattern","COPY",BODY,{"derivedFrom":makeQuery(id+"F2.opPattern","COPY",BODY,{"derivedFrom":makeQuery(id+"F1.opRevolve","SWEPT_BODY",BODY,{"disambiguationData":[OSD([sQuery(id+"F0.wireOp",EDGE,"E1")])]}),"instanceName":"1"}),"instanceName":"1"}),"instanceName":"1"}),"instanceName":"1"}),"instanceName":"1"}),"instanceName":"1"}),"instanceName":"1"}),"instanceName":"1"});
            var Q731;
            Q731=makeQuery(id+"F11.opPattern","COPY",BODY,{"derivedFrom":makeQuery(id+"F10.opPattern","COPY",BODY,{"derivedFrom":makeQuery(id+"F9.opPattern","COPY",BODY,{"derivedFrom":makeQuery(id+"F8.opPattern","COPY",BODY,{"derivedFrom":makeQuery(id+"F6.opPattern","COPY",BODY,{"derivedFrom":makeQuery(id+"F1.opRevolve","SWEPT_BODY",BODY,{"disambiguationData":[OSD([sQuery(id+"F0.wireOp",EDGE,"E1")])]}),"instanceName":"1"}),"instanceName":"1"}),"instanceName":"1"}),"instanceName":"1"}),"instanceName":"1"});
            var Q732;
            Q732=makeQuery(id+"F11.opPattern","COPY",BODY,{"derivedFrom":makeQuery(id+"F10.opPattern","COPY",BODY,{"derivedFrom":makeQuery(id+"F9.opPattern","COPY",BODY,{"derivedFrom":makeQuery(id+"F8.opPattern","COPY",BODY,{"derivedFrom":makeQuery(id+"F6.opPattern","COPY",BODY,{"derivedFrom":makeQuery(id+"F2.opPattern","COPY",BODY,{"derivedFrom":makeQuery(id+"F1.opRevolve","SWEPT_BODY",BODY,{"disambiguationData":[OSD([sQuery(id+"F0.wireOp",EDGE,"E1")])]}),"instanceName":"1"}),"instanceName":"1"}),"instanceName":"1"}),"instanceName":"1"}),"instanceName":"1"}),"instanceName":"1"});
            var Q733;
            Q733=makeQuery(id+"F11.opPattern","COPY",BODY,{"derivedFrom":makeQuery(id+"F10.opPattern","COPY",BODY,{"derivedFrom":makeQuery(id+"F9.opPattern","COPY",BODY,{"derivedFrom":makeQuery(id+"F8.opPattern","COPY",BODY,{"derivedFrom":makeQuery(id+"F6.opPattern","COPY",BODY,{"derivedFrom":makeQuery(id+"F3.opPattern","COPY",BODY,{"derivedFrom":makeQuery(id+"F2.opPattern","COPY",BODY,{"derivedFrom":makeQuery(id+"F1.opRevolve","SWEPT_BODY",BODY,{"disambiguationData":[OSD([sQuery(id+"F0.wireOp",EDGE,"E1")])]}),"instanceName":"1"}),"instanceName":"1"}),"instanceName":"1"}),"instanceName":"1"}),"instanceName":"1"}),"instanceName":"1"}),"instanceName":"1"});
            var Q734;
            Q734=makeQuery(id+"F11.opPattern","COPY",BODY,{"derivedFrom":makeQuery(id+"F10.opPattern","COPY",BODY,{"derivedFrom":makeQuery(id+"F9.opPattern","COPY",BODY,{"derivedFrom":makeQuery(id+"F8.opPattern","COPY",BODY,{"derivedFrom":makeQuery(id+"F6.opPattern","COPY",BODY,{"derivedFrom":makeQuery(id+"F4.opPattern","COPY",BODY,{"derivedFrom":makeQuery(id+"F1.opRevolve","SWEPT_BODY",BODY,{"disambiguationData":[OSD([sQuery(id+"F0.wireOp",EDGE,"E1")])]}),"instanceName":"1"}),"instanceName":"1"}),"instanceName":"1"}),"instanceName":"1"}),"instanceName":"1"}),"instanceName":"1"});
            var Q735;
            Q735=makeQuery(id+"F11.opPattern","COPY",BODY,{"derivedFrom":makeQuery(id+"F10.opPattern","COPY",BODY,{"derivedFrom":makeQuery(id+"F9.opPattern","COPY",BODY,{"derivedFrom":makeQuery(id+"F8.opPattern","COPY",BODY,{"derivedFrom":makeQuery(id+"F6.opPattern","COPY",BODY,{"derivedFrom":makeQuery(id+"F4.opPattern","COPY",BODY,{"derivedFrom":makeQuery(id+"F2.opPattern","COPY",BODY,{"derivedFrom":makeQuery(id+"F1.opRevolve","SWEPT_BODY",BODY,{"disambiguationData":[OSD([sQuery(id+"F0.wireOp",EDGE,"E1")])]}),"instanceName":"1"}),"instanceName":"1"}),"instanceName":"1"}),"instanceName":"1"}),"instanceName":"1"}),"instanceName":"1"}),"instanceName":"1"});
            var Q736;
            Q736=makeQuery(id+"F11.opPattern","COPY",BODY,{"derivedFrom":makeQuery(id+"F10.opPattern","COPY",BODY,{"derivedFrom":makeQuery(id+"F9.opPattern","COPY",BODY,{"derivedFrom":makeQuery(id+"F8.opPattern","COPY",BODY,{"derivedFrom":makeQuery(id+"F6.opPattern","COPY",BODY,{"derivedFrom":makeQuery(id+"F4.opPattern","COPY",BODY,{"derivedFrom":makeQuery(id+"F3.opPattern","COPY",BODY,{"derivedFrom":makeQuery(id+"F2.opPattern","COPY",BODY,{"derivedFrom":makeQuery(id+"F1.opRevolve","SWEPT_BODY",BODY,{"disambiguationData":[OSD([sQuery(id+"F0.wireOp",EDGE,"E1")])]}),"instanceName":"1"}),"instanceName":"1"}),"instanceName":"1"}),"instanceName":"1"}),"instanceName":"1"}),"instanceName":"1"}),"instanceName":"1"}),"instanceName":"1"});
            var Q737;
            Q737=makeQuery(id+"F11.opPattern","COPY",BODY,{"derivedFrom":makeQuery(id+"F10.opPattern","COPY",BODY,{"derivedFrom":makeQuery(id+"F9.opPattern","COPY",BODY,{"derivedFrom":makeQuery(id+"F8.opPattern","COPY",BODY,{"derivedFrom":makeQuery(id+"F6.opPattern","COPY",BODY,{"derivedFrom":makeQuery(id+"F5.opPattern","COPY",BODY,{"derivedFrom":makeQuery(id+"F1.opRevolve","SWEPT_BODY",BODY,{"disambiguationData":[OSD([sQuery(id+"F0.wireOp",EDGE,"E1")])]}),"instanceName":"1"}),"instanceName":"1"}),"instanceName":"1"}),"instanceName":"1"}),"instanceName":"1"}),"instanceName":"1"});
            var Q738;
            Q738=makeQuery(id+"F11.opPattern","COPY",BODY,{"derivedFrom":makeQuery(id+"F10.opPattern","COPY",BODY,{"derivedFrom":makeQuery(id+"F9.opPattern","COPY",BODY,{"derivedFrom":makeQuery(id+"F8.opPattern","COPY",BODY,{"derivedFrom":makeQuery(id+"F6.opPattern","COPY",BODY,{"derivedFrom":makeQuery(id+"F5.opPattern","COPY",BODY,{"derivedFrom":makeQuery(id+"F2.opPattern","COPY",BODY,{"derivedFrom":makeQuery(id+"F1.opRevolve","SWEPT_BODY",BODY,{"disambiguationData":[OSD([sQuery(id+"F0.wireOp",EDGE,"E1")])]}),"instanceName":"1"}),"instanceName":"1"}),"instanceName":"1"}),"instanceName":"1"}),"instanceName":"1"}),"instanceName":"1"}),"instanceName":"1"});
            var Q739;
            Q739=makeQuery(id+"F11.opPattern","COPY",BODY,{"derivedFrom":makeQuery(id+"F10.opPattern","COPY",BODY,{"derivedFrom":makeQuery(id+"F9.opPattern","COPY",BODY,{"derivedFrom":makeQuery(id+"F8.opPattern","COPY",BODY,{"derivedFrom":makeQuery(id+"F6.opPattern","COPY",BODY,{"derivedFrom":makeQuery(id+"F5.opPattern","COPY",BODY,{"derivedFrom":makeQuery(id+"F3.opPattern","COPY",BODY,{"derivedFrom":makeQuery(id+"F2.opPattern","COPY",BODY,{"derivedFrom":makeQuery(id+"F1.opRevolve","SWEPT_BODY",BODY,{"disambiguationData":[OSD([sQuery(id+"F0.wireOp",EDGE,"E1")])]}),"instanceName":"1"}),"instanceName":"1"}),"instanceName":"1"}),"instanceName":"1"}),"instanceName":"1"}),"instanceName":"1"}),"instanceName":"1"}),"instanceName":"1"});
            var Q740;
            Q740=makeQuery(id+"F11.opPattern","COPY",BODY,{"derivedFrom":makeQuery(id+"F10.opPattern","COPY",BODY,{"derivedFrom":makeQuery(id+"F9.opPattern","COPY",BODY,{"derivedFrom":makeQuery(id+"F8.opPattern","COPY",BODY,{"derivedFrom":makeQuery(id+"F6.opPattern","COPY",BODY,{"derivedFrom":makeQuery(id+"F5.opPattern","COPY",BODY,{"derivedFrom":makeQuery(id+"F4.opPattern","COPY",BODY,{"derivedFrom":makeQuery(id+"F1.opRevolve","SWEPT_BODY",BODY,{"disambiguationData":[OSD([sQuery(id+"F0.wireOp",EDGE,"E1")])]}),"instanceName":"1"}),"instanceName":"1"}),"instanceName":"1"}),"instanceName":"1"}),"instanceName":"1"}),"instanceName":"1"}),"instanceName":"1"});
            var Q741;
            Q741=makeQuery(id+"F11.opPattern","COPY",BODY,{"derivedFrom":makeQuery(id+"F10.opPattern","COPY",BODY,{"derivedFrom":makeQuery(id+"F9.opPattern","COPY",BODY,{"derivedFrom":makeQuery(id+"F8.opPattern","COPY",BODY,{"derivedFrom":makeQuery(id+"F6.opPattern","COPY",BODY,{"derivedFrom":makeQuery(id+"F5.opPattern","COPY",BODY,{"derivedFrom":makeQuery(id+"F4.opPattern","COPY",BODY,{"derivedFrom":makeQuery(id+"F2.opPattern","COPY",BODY,{"derivedFrom":makeQuery(id+"F1.opRevolve","SWEPT_BODY",BODY,{"disambiguationData":[OSD([sQuery(id+"F0.wireOp",EDGE,"E1")])]}),"instanceName":"1"}),"instanceName":"1"}),"instanceName":"1"}),"instanceName":"1"}),"instanceName":"1"}),"instanceName":"1"}),"instanceName":"1"}),"instanceName":"1"});
            var Q742;
            Q742=makeQuery(id+"F11.opPattern","COPY",BODY,{"derivedFrom":makeQuery(id+"F10.opPattern","COPY",BODY,{"derivedFrom":makeQuery(id+"F9.opPattern","COPY",BODY,{"derivedFrom":makeQuery(id+"F8.opPattern","COPY",BODY,{"derivedFrom":makeQuery(id+"F6.opPattern","COPY",BODY,{"derivedFrom":makeQuery(id+"F5.opPattern","COPY",BODY,{"derivedFrom":makeQuery(id+"F4.opPattern","COPY",BODY,{"derivedFrom":makeQuery(id+"F3.opPattern","COPY",BODY,{"derivedFrom":makeQuery(id+"F2.opPattern","COPY",BODY,{"derivedFrom":makeQuery(id+"F1.opRevolve","SWEPT_BODY",BODY,{"disambiguationData":[OSD([sQuery(id+"F0.wireOp",EDGE,"E1")])]}),"instanceName":"1"}),"instanceName":"1"}),"instanceName":"1"}),"instanceName":"1"}),"instanceName":"1"}),"instanceName":"1"}),"instanceName":"1"}),"instanceName":"1"}),"instanceName":"1"});
            var Q743;
            Q743=makeQuery(id+"F11.opPattern","COPY",BODY,{"derivedFrom":makeQuery(id+"F10.opPattern","COPY",BODY,{"derivedFrom":makeQuery(id+"F9.opPattern","COPY",BODY,{"derivedFrom":makeQuery(id+"F8.opPattern","COPY",BODY,{"derivedFrom":makeQuery(id+"F7.opPattern","COPY",BODY,{"derivedFrom":makeQuery(id+"F1.opRevolve","SWEPT_BODY",BODY,{"disambiguationData":[OSD([sQuery(id+"F0.wireOp",EDGE,"E1")])]}),"instanceName":"1"}),"instanceName":"1"}),"instanceName":"1"}),"instanceName":"1"}),"instanceName":"1"});
            var Q744;
            Q744=makeQuery(id+"F11.opPattern","COPY",BODY,{"derivedFrom":makeQuery(id+"F10.opPattern","COPY",BODY,{"derivedFrom":makeQuery(id+"F9.opPattern","COPY",BODY,{"derivedFrom":makeQuery(id+"F8.opPattern","COPY",BODY,{"derivedFrom":makeQuery(id+"F7.opPattern","COPY",BODY,{"derivedFrom":makeQuery(id+"F2.opPattern","COPY",BODY,{"derivedFrom":makeQuery(id+"F1.opRevolve","SWEPT_BODY",BODY,{"disambiguationData":[OSD([sQuery(id+"F0.wireOp",EDGE,"E1")])]}),"instanceName":"1"}),"instanceName":"1"}),"instanceName":"1"}),"instanceName":"1"}),"instanceName":"1"}),"instanceName":"1"});
            var Q745;
            Q745=makeQuery(id+"F11.opPattern","COPY",BODY,{"derivedFrom":makeQuery(id+"F10.opPattern","COPY",BODY,{"derivedFrom":makeQuery(id+"F9.opPattern","COPY",BODY,{"derivedFrom":makeQuery(id+"F8.opPattern","COPY",BODY,{"derivedFrom":makeQuery(id+"F7.opPattern","COPY",BODY,{"derivedFrom":makeQuery(id+"F3.opPattern","COPY",BODY,{"derivedFrom":makeQuery(id+"F2.opPattern","COPY",BODY,{"derivedFrom":makeQuery(id+"F1.opRevolve","SWEPT_BODY",BODY,{"disambiguationData":[OSD([sQuery(id+"F0.wireOp",EDGE,"E1")])]}),"instanceName":"1"}),"instanceName":"1"}),"instanceName":"1"}),"instanceName":"1"}),"instanceName":"1"}),"instanceName":"1"}),"instanceName":"1"});
            var Q746;
            Q746=makeQuery(id+"F11.opPattern","COPY",BODY,{"derivedFrom":makeQuery(id+"F10.opPattern","COPY",BODY,{"derivedFrom":makeQuery(id+"F9.opPattern","COPY",BODY,{"derivedFrom":makeQuery(id+"F8.opPattern","COPY",BODY,{"derivedFrom":makeQuery(id+"F7.opPattern","COPY",BODY,{"derivedFrom":makeQuery(id+"F4.opPattern","COPY",BODY,{"derivedFrom":makeQuery(id+"F1.opRevolve","SWEPT_BODY",BODY,{"disambiguationData":[OSD([sQuery(id+"F0.wireOp",EDGE,"E1")])]}),"instanceName":"1"}),"instanceName":"1"}),"instanceName":"1"}),"instanceName":"1"}),"instanceName":"1"}),"instanceName":"1"});
            var Q747;
            Q747=makeQuery(id+"F11.opPattern","COPY",BODY,{"derivedFrom":makeQuery(id+"F10.opPattern","COPY",BODY,{"derivedFrom":makeQuery(id+"F9.opPattern","COPY",BODY,{"derivedFrom":makeQuery(id+"F8.opPattern","COPY",BODY,{"derivedFrom":makeQuery(id+"F7.opPattern","COPY",BODY,{"derivedFrom":makeQuery(id+"F4.opPattern","COPY",BODY,{"derivedFrom":makeQuery(id+"F2.opPattern","COPY",BODY,{"derivedFrom":makeQuery(id+"F1.opRevolve","SWEPT_BODY",BODY,{"disambiguationData":[OSD([sQuery(id+"F0.wireOp",EDGE,"E1")])]}),"instanceName":"1"}),"instanceName":"1"}),"instanceName":"1"}),"instanceName":"1"}),"instanceName":"1"}),"instanceName":"1"}),"instanceName":"1"});
            var Q748;
            Q748=makeQuery(id+"F11.opPattern","COPY",BODY,{"derivedFrom":makeQuery(id+"F10.opPattern","COPY",BODY,{"derivedFrom":makeQuery(id+"F9.opPattern","COPY",BODY,{"derivedFrom":makeQuery(id+"F8.opPattern","COPY",BODY,{"derivedFrom":makeQuery(id+"F7.opPattern","COPY",BODY,{"derivedFrom":makeQuery(id+"F4.opPattern","COPY",BODY,{"derivedFrom":makeQuery(id+"F3.opPattern","COPY",BODY,{"derivedFrom":makeQuery(id+"F2.opPattern","COPY",BODY,{"derivedFrom":makeQuery(id+"F1.opRevolve","SWEPT_BODY",BODY,{"disambiguationData":[OSD([sQuery(id+"F0.wireOp",EDGE,"E1")])]}),"instanceName":"1"}),"instanceName":"1"}),"instanceName":"1"}),"instanceName":"1"}),"instanceName":"1"}),"instanceName":"1"}),"instanceName":"1"}),"instanceName":"1"});
            var Q749;
            Q749=makeQuery(id+"F11.opPattern","COPY",BODY,{"derivedFrom":makeQuery(id+"F10.opPattern","COPY",BODY,{"derivedFrom":makeQuery(id+"F9.opPattern","COPY",BODY,{"derivedFrom":makeQuery(id+"F8.opPattern","COPY",BODY,{"derivedFrom":makeQuery(id+"F7.opPattern","COPY",BODY,{"derivedFrom":makeQuery(id+"F5.opPattern","COPY",BODY,{"derivedFrom":makeQuery(id+"F1.opRevolve","SWEPT_BODY",BODY,{"disambiguationData":[OSD([sQuery(id+"F0.wireOp",EDGE,"E1")])]}),"instanceName":"1"}),"instanceName":"1"}),"instanceName":"1"}),"instanceName":"1"}),"instanceName":"1"}),"instanceName":"1"});
            var Q750;
            Q750=makeQuery(id+"F11.opPattern","COPY",BODY,{"derivedFrom":makeQuery(id+"F10.opPattern","COPY",BODY,{"derivedFrom":makeQuery(id+"F9.opPattern","COPY",BODY,{"derivedFrom":makeQuery(id+"F8.opPattern","COPY",BODY,{"derivedFrom":makeQuery(id+"F7.opPattern","COPY",BODY,{"derivedFrom":makeQuery(id+"F5.opPattern","COPY",BODY,{"derivedFrom":makeQuery(id+"F2.opPattern","COPY",BODY,{"derivedFrom":makeQuery(id+"F1.opRevolve","SWEPT_BODY",BODY,{"disambiguationData":[OSD([sQuery(id+"F0.wireOp",EDGE,"E1")])]}),"instanceName":"1"}),"instanceName":"1"}),"instanceName":"1"}),"instanceName":"1"}),"instanceName":"1"}),"instanceName":"1"}),"instanceName":"1"});
            var Q751;
            Q751=makeQuery(id+"F11.opPattern","COPY",BODY,{"derivedFrom":makeQuery(id+"F10.opPattern","COPY",BODY,{"derivedFrom":makeQuery(id+"F9.opPattern","COPY",BODY,{"derivedFrom":makeQuery(id+"F8.opPattern","COPY",BODY,{"derivedFrom":makeQuery(id+"F7.opPattern","COPY",BODY,{"derivedFrom":makeQuery(id+"F5.opPattern","COPY",BODY,{"derivedFrom":makeQuery(id+"F3.opPattern","COPY",BODY,{"derivedFrom":makeQuery(id+"F2.opPattern","COPY",BODY,{"derivedFrom":makeQuery(id+"F1.opRevolve","SWEPT_BODY",BODY,{"disambiguationData":[OSD([sQuery(id+"F0.wireOp",EDGE,"E1")])]}),"instanceName":"1"}),"instanceName":"1"}),"instanceName":"1"}),"instanceName":"1"}),"instanceName":"1"}),"instanceName":"1"}),"instanceName":"1"}),"instanceName":"1"});
            var Q752;
            Q752=makeQuery(id+"F11.opPattern","COPY",BODY,{"derivedFrom":makeQuery(id+"F10.opPattern","COPY",BODY,{"derivedFrom":makeQuery(id+"F9.opPattern","COPY",BODY,{"derivedFrom":makeQuery(id+"F8.opPattern","COPY",BODY,{"derivedFrom":makeQuery(id+"F7.opPattern","COPY",BODY,{"derivedFrom":makeQuery(id+"F5.opPattern","COPY",BODY,{"derivedFrom":makeQuery(id+"F4.opPattern","COPY",BODY,{"derivedFrom":makeQuery(id+"F1.opRevolve","SWEPT_BODY",BODY,{"disambiguationData":[OSD([sQuery(id+"F0.wireOp",EDGE,"E1")])]}),"instanceName":"1"}),"instanceName":"1"}),"instanceName":"1"}),"instanceName":"1"}),"instanceName":"1"}),"instanceName":"1"}),"instanceName":"1"});
            var Q753;
            Q753=makeQuery(id+"F11.opPattern","COPY",BODY,{"derivedFrom":makeQuery(id+"F10.opPattern","COPY",BODY,{"derivedFrom":makeQuery(id+"F9.opPattern","COPY",BODY,{"derivedFrom":makeQuery(id+"F8.opPattern","COPY",BODY,{"derivedFrom":makeQuery(id+"F7.opPattern","COPY",BODY,{"derivedFrom":makeQuery(id+"F5.opPattern","COPY",BODY,{"derivedFrom":makeQuery(id+"F4.opPattern","COPY",BODY,{"derivedFrom":makeQuery(id+"F2.opPattern","COPY",BODY,{"derivedFrom":makeQuery(id+"F1.opRevolve","SWEPT_BODY",BODY,{"disambiguationData":[OSD([sQuery(id+"F0.wireOp",EDGE,"E1")])]}),"instanceName":"1"}),"instanceName":"1"}),"instanceName":"1"}),"instanceName":"1"}),"instanceName":"1"}),"instanceName":"1"}),"instanceName":"1"}),"instanceName":"1"});
            var Q754;
            Q754=makeQuery(id+"F11.opPattern","COPY",BODY,{"derivedFrom":makeQuery(id+"F10.opPattern","COPY",BODY,{"derivedFrom":makeQuery(id+"F9.opPattern","COPY",BODY,{"derivedFrom":makeQuery(id+"F8.opPattern","COPY",BODY,{"derivedFrom":makeQuery(id+"F7.opPattern","COPY",BODY,{"derivedFrom":makeQuery(id+"F5.opPattern","COPY",BODY,{"derivedFrom":makeQuery(id+"F4.opPattern","COPY",BODY,{"derivedFrom":makeQuery(id+"F3.opPattern","COPY",BODY,{"derivedFrom":makeQuery(id+"F2.opPattern","COPY",BODY,{"derivedFrom":makeQuery(id+"F1.opRevolve","SWEPT_BODY",BODY,{"disambiguationData":[OSD([sQuery(id+"F0.wireOp",EDGE,"E1")])]}),"instanceName":"1"}),"instanceName":"1"}),"instanceName":"1"}),"instanceName":"1"}),"instanceName":"1"}),"instanceName":"1"}),"instanceName":"1"}),"instanceName":"1"}),"instanceName":"1"});
            var Q755;
            Q755=makeQuery(id+"F11.opPattern","COPY",BODY,{"derivedFrom":makeQuery(id+"F10.opPattern","COPY",BODY,{"derivedFrom":makeQuery(id+"F9.opPattern","COPY",BODY,{"derivedFrom":makeQuery(id+"F8.opPattern","COPY",BODY,{"derivedFrom":makeQuery(id+"F7.opPattern","COPY",BODY,{"derivedFrom":makeQuery(id+"F6.opPattern","COPY",BODY,{"derivedFrom":makeQuery(id+"F1.opRevolve","SWEPT_BODY",BODY,{"disambiguationData":[OSD([sQuery(id+"F0.wireOp",EDGE,"E1")])]}),"instanceName":"1"}),"instanceName":"1"}),"instanceName":"1"}),"instanceName":"1"}),"instanceName":"1"}),"instanceName":"1"});
            var Q756;
            Q756=makeQuery(id+"F11.opPattern","COPY",BODY,{"derivedFrom":makeQuery(id+"F10.opPattern","COPY",BODY,{"derivedFrom":makeQuery(id+"F9.opPattern","COPY",BODY,{"derivedFrom":makeQuery(id+"F8.opPattern","COPY",BODY,{"derivedFrom":makeQuery(id+"F7.opPattern","COPY",BODY,{"derivedFrom":makeQuery(id+"F6.opPattern","COPY",BODY,{"derivedFrom":makeQuery(id+"F2.opPattern","COPY",BODY,{"derivedFrom":makeQuery(id+"F1.opRevolve","SWEPT_BODY",BODY,{"disambiguationData":[OSD([sQuery(id+"F0.wireOp",EDGE,"E1")])]}),"instanceName":"1"}),"instanceName":"1"}),"instanceName":"1"}),"instanceName":"1"}),"instanceName":"1"}),"instanceName":"1"}),"instanceName":"1"});
            var Q757;
            Q757=makeQuery(id+"F11.opPattern","COPY",BODY,{"derivedFrom":makeQuery(id+"F10.opPattern","COPY",BODY,{"derivedFrom":makeQuery(id+"F9.opPattern","COPY",BODY,{"derivedFrom":makeQuery(id+"F8.opPattern","COPY",BODY,{"derivedFrom":makeQuery(id+"F7.opPattern","COPY",BODY,{"derivedFrom":makeQuery(id+"F6.opPattern","COPY",BODY,{"derivedFrom":makeQuery(id+"F3.opPattern","COPY",BODY,{"derivedFrom":makeQuery(id+"F2.opPattern","COPY",BODY,{"derivedFrom":makeQuery(id+"F1.opRevolve","SWEPT_BODY",BODY,{"disambiguationData":[OSD([sQuery(id+"F0.wireOp",EDGE,"E1")])]}),"instanceName":"1"}),"instanceName":"1"}),"instanceName":"1"}),"instanceName":"1"}),"instanceName":"1"}),"instanceName":"1"}),"instanceName":"1"}),"instanceName":"1"});
            var Q758;
            Q758=makeQuery(id+"F11.opPattern","COPY",BODY,{"derivedFrom":makeQuery(id+"F10.opPattern","COPY",BODY,{"derivedFrom":makeQuery(id+"F9.opPattern","COPY",BODY,{"derivedFrom":makeQuery(id+"F8.opPattern","COPY",BODY,{"derivedFrom":makeQuery(id+"F7.opPattern","COPY",BODY,{"derivedFrom":makeQuery(id+"F6.opPattern","COPY",BODY,{"derivedFrom":makeQuery(id+"F4.opPattern","COPY",BODY,{"derivedFrom":makeQuery(id+"F1.opRevolve","SWEPT_BODY",BODY,{"disambiguationData":[OSD([sQuery(id+"F0.wireOp",EDGE,"E1")])]}),"instanceName":"1"}),"instanceName":"1"}),"instanceName":"1"}),"instanceName":"1"}),"instanceName":"1"}),"instanceName":"1"}),"instanceName":"1"});
            var Q759;
            Q759=makeQuery(id+"F11.opPattern","COPY",BODY,{"derivedFrom":makeQuery(id+"F10.opPattern","COPY",BODY,{"derivedFrom":makeQuery(id+"F9.opPattern","COPY",BODY,{"derivedFrom":makeQuery(id+"F8.opPattern","COPY",BODY,{"derivedFrom":makeQuery(id+"F7.opPattern","COPY",BODY,{"derivedFrom":makeQuery(id+"F6.opPattern","COPY",BODY,{"derivedFrom":makeQuery(id+"F4.opPattern","COPY",BODY,{"derivedFrom":makeQuery(id+"F2.opPattern","COPY",BODY,{"derivedFrom":makeQuery(id+"F1.opRevolve","SWEPT_BODY",BODY,{"disambiguationData":[OSD([sQuery(id+"F0.wireOp",EDGE,"E1")])]}),"instanceName":"1"}),"instanceName":"1"}),"instanceName":"1"}),"instanceName":"1"}),"instanceName":"1"}),"instanceName":"1"}),"instanceName":"1"}),"instanceName":"1"});
            var Q760;
            Q760=makeQuery(id+"F11.opPattern","COPY",BODY,{"derivedFrom":makeQuery(id+"F10.opPattern","COPY",BODY,{"derivedFrom":makeQuery(id+"F9.opPattern","COPY",BODY,{"derivedFrom":makeQuery(id+"F8.opPattern","COPY",BODY,{"derivedFrom":makeQuery(id+"F7.opPattern","COPY",BODY,{"derivedFrom":makeQuery(id+"F6.opPattern","COPY",BODY,{"derivedFrom":makeQuery(id+"F4.opPattern","COPY",BODY,{"derivedFrom":makeQuery(id+"F3.opPattern","COPY",BODY,{"derivedFrom":makeQuery(id+"F2.opPattern","COPY",BODY,{"derivedFrom":makeQuery(id+"F1.opRevolve","SWEPT_BODY",BODY,{"disambiguationData":[OSD([sQuery(id+"F0.wireOp",EDGE,"E1")])]}),"instanceName":"1"}),"instanceName":"1"}),"instanceName":"1"}),"instanceName":"1"}),"instanceName":"1"}),"instanceName":"1"}),"instanceName":"1"}),"instanceName":"1"}),"instanceName":"1"});
            var Q761;
            Q761=makeQuery(id+"F11.opPattern","COPY",BODY,{"derivedFrom":makeQuery(id+"F10.opPattern","COPY",BODY,{"derivedFrom":makeQuery(id+"F9.opPattern","COPY",BODY,{"derivedFrom":makeQuery(id+"F8.opPattern","COPY",BODY,{"derivedFrom":makeQuery(id+"F7.opPattern","COPY",BODY,{"derivedFrom":makeQuery(id+"F6.opPattern","COPY",BODY,{"derivedFrom":makeQuery(id+"F5.opPattern","COPY",BODY,{"derivedFrom":makeQuery(id+"F1.opRevolve","SWEPT_BODY",BODY,{"disambiguationData":[OSD([sQuery(id+"F0.wireOp",EDGE,"E1")])]}),"instanceName":"1"}),"instanceName":"1"}),"instanceName":"1"}),"instanceName":"1"}),"instanceName":"1"}),"instanceName":"1"}),"instanceName":"1"});
            var Q762;
            Q762=makeQuery(id+"F11.opPattern","COPY",BODY,{"derivedFrom":makeQuery(id+"F10.opPattern","COPY",BODY,{"derivedFrom":makeQuery(id+"F9.opPattern","COPY",BODY,{"derivedFrom":makeQuery(id+"F8.opPattern","COPY",BODY,{"derivedFrom":makeQuery(id+"F7.opPattern","COPY",BODY,{"derivedFrom":makeQuery(id+"F6.opPattern","COPY",BODY,{"derivedFrom":makeQuery(id+"F5.opPattern","COPY",BODY,{"derivedFrom":makeQuery(id+"F2.opPattern","COPY",BODY,{"derivedFrom":makeQuery(id+"F1.opRevolve","SWEPT_BODY",BODY,{"disambiguationData":[OSD([sQuery(id+"F0.wireOp",EDGE,"E1")])]}),"instanceName":"1"}),"instanceName":"1"}),"instanceName":"1"}),"instanceName":"1"}),"instanceName":"1"}),"instanceName":"1"}),"instanceName":"1"}),"instanceName":"1"});
            var Q763;
            Q763=makeQuery(id+"F11.opPattern","COPY",BODY,{"derivedFrom":makeQuery(id+"F10.opPattern","COPY",BODY,{"derivedFrom":makeQuery(id+"F9.opPattern","COPY",BODY,{"derivedFrom":makeQuery(id+"F8.opPattern","COPY",BODY,{"derivedFrom":makeQuery(id+"F7.opPattern","COPY",BODY,{"derivedFrom":makeQuery(id+"F6.opPattern","COPY",BODY,{"derivedFrom":makeQuery(id+"F5.opPattern","COPY",BODY,{"derivedFrom":makeQuery(id+"F3.opPattern","COPY",BODY,{"derivedFrom":makeQuery(id+"F2.opPattern","COPY",BODY,{"derivedFrom":makeQuery(id+"F1.opRevolve","SWEPT_BODY",BODY,{"disambiguationData":[OSD([sQuery(id+"F0.wireOp",EDGE,"E1")])]}),"instanceName":"1"}),"instanceName":"1"}),"instanceName":"1"}),"instanceName":"1"}),"instanceName":"1"}),"instanceName":"1"}),"instanceName":"1"}),"instanceName":"1"}),"instanceName":"1"});
            var Q764;
            Q764=makeQuery(id+"F11.opPattern","COPY",BODY,{"derivedFrom":makeQuery(id+"F10.opPattern","COPY",BODY,{"derivedFrom":makeQuery(id+"F9.opPattern","COPY",BODY,{"derivedFrom":makeQuery(id+"F8.opPattern","COPY",BODY,{"derivedFrom":makeQuery(id+"F7.opPattern","COPY",BODY,{"derivedFrom":makeQuery(id+"F6.opPattern","COPY",BODY,{"derivedFrom":makeQuery(id+"F5.opPattern","COPY",BODY,{"derivedFrom":makeQuery(id+"F4.opPattern","COPY",BODY,{"derivedFrom":makeQuery(id+"F1.opRevolve","SWEPT_BODY",BODY,{"disambiguationData":[OSD([sQuery(id+"F0.wireOp",EDGE,"E1")])]}),"instanceName":"1"}),"instanceName":"1"}),"instanceName":"1"}),"instanceName":"1"}),"instanceName":"1"}),"instanceName":"1"}),"instanceName":"1"}),"instanceName":"1"});
            var Q765;
            Q765=makeQuery(id+"F11.opPattern","COPY",BODY,{"derivedFrom":makeQuery(id+"F10.opPattern","COPY",BODY,{"derivedFrom":makeQuery(id+"F9.opPattern","COPY",BODY,{"derivedFrom":makeQuery(id+"F8.opPattern","COPY",BODY,{"derivedFrom":makeQuery(id+"F7.opPattern","COPY",BODY,{"derivedFrom":makeQuery(id+"F6.opPattern","COPY",BODY,{"derivedFrom":makeQuery(id+"F5.opPattern","COPY",BODY,{"derivedFrom":makeQuery(id+"F4.opPattern","COPY",BODY,{"derivedFrom":makeQuery(id+"F2.opPattern","COPY",BODY,{"derivedFrom":makeQuery(id+"F1.opRevolve","SWEPT_BODY",BODY,{"disambiguationData":[OSD([sQuery(id+"F0.wireOp",EDGE,"E1")])]}),"instanceName":"1"}),"instanceName":"1"}),"instanceName":"1"}),"instanceName":"1"}),"instanceName":"1"}),"instanceName":"1"}),"instanceName":"1"}),"instanceName":"1"}),"instanceName":"1"});
            var Q766;
            Q766=makeQuery(id+"F11.opPattern","COPY",BODY,{"derivedFrom":makeQuery(id+"F10.opPattern","COPY",BODY,{"derivedFrom":makeQuery(id+"F9.opPattern","COPY",BODY,{"derivedFrom":makeQuery(id+"F8.opPattern","COPY",BODY,{"derivedFrom":makeQuery(id+"F7.opPattern","COPY",BODY,{"derivedFrom":makeQuery(id+"F6.opPattern","COPY",BODY,{"derivedFrom":makeQuery(id+"F5.opPattern","COPY",BODY,{"derivedFrom":makeQuery(id+"F4.opPattern","COPY",BODY,{"derivedFrom":makeQuery(id+"F3.opPattern","COPY",BODY,{"derivedFrom":makeQuery(id+"F2.opPattern","COPY",BODY,{"derivedFrom":makeQuery(id+"F1.opRevolve","SWEPT_BODY",BODY,{"disambiguationData":[OSD([sQuery(id+"F0.wireOp",EDGE,"E1")])]}),"instanceName":"1"}),"instanceName":"1"}),"instanceName":"1"}),"instanceName":"1"}),"instanceName":"1"}),"instanceName":"1"}),"instanceName":"1"}),"instanceName":"1"}),"instanceName":"1"}),"instanceName":"1"});
            var Q767;
            Q767=makeQuery(id+"F12.opPattern","COPY",BODY,{"derivedFrom":makeQuery(id+"F1.opRevolve","SWEPT_BODY",BODY,{"disambiguationData":[OSD([sQuery(id+"F0.wireOp",EDGE,"E1")])]}),"instanceName":"1"});
            var Q768;
            Q768=makeQuery(id+"F12.opPattern","COPY",BODY,{"derivedFrom":makeQuery(id+"F2.opPattern","COPY",BODY,{"derivedFrom":makeQuery(id+"F1.opRevolve","SWEPT_BODY",BODY,{"disambiguationData":[OSD([sQuery(id+"F0.wireOp",EDGE,"E1")])]}),"instanceName":"1"}),"instanceName":"1"});
            var Q769;
            Q769=makeQuery(id+"F12.opPattern","COPY",BODY,{"derivedFrom":makeQuery(id+"F3.opPattern","COPY",BODY,{"derivedFrom":makeQuery(id+"F2.opPattern","COPY",BODY,{"derivedFrom":makeQuery(id+"F1.opRevolve","SWEPT_BODY",BODY,{"disambiguationData":[OSD([sQuery(id+"F0.wireOp",EDGE,"E1")])]}),"instanceName":"1"}),"instanceName":"1"}),"instanceName":"1"});
            var Q770;
            Q770=makeQuery(id+"F12.opPattern","COPY",BODY,{"derivedFrom":makeQuery(id+"F4.opPattern","COPY",BODY,{"derivedFrom":makeQuery(id+"F1.opRevolve","SWEPT_BODY",BODY,{"disambiguationData":[OSD([sQuery(id+"F0.wireOp",EDGE,"E1")])]}),"instanceName":"1"}),"instanceName":"1"});
            var Q771;
            Q771=makeQuery(id+"F12.opPattern","COPY",BODY,{"derivedFrom":makeQuery(id+"F4.opPattern","COPY",BODY,{"derivedFrom":makeQuery(id+"F2.opPattern","COPY",BODY,{"derivedFrom":makeQuery(id+"F1.opRevolve","SWEPT_BODY",BODY,{"disambiguationData":[OSD([sQuery(id+"F0.wireOp",EDGE,"E1")])]}),"instanceName":"1"}),"instanceName":"1"}),"instanceName":"1"});
            var Q772;
            Q772=makeQuery(id+"F12.opPattern","COPY",BODY,{"derivedFrom":makeQuery(id+"F4.opPattern","COPY",BODY,{"derivedFrom":makeQuery(id+"F3.opPattern","COPY",BODY,{"derivedFrom":makeQuery(id+"F2.opPattern","COPY",BODY,{"derivedFrom":makeQuery(id+"F1.opRevolve","SWEPT_BODY",BODY,{"disambiguationData":[OSD([sQuery(id+"F0.wireOp",EDGE,"E1")])]}),"instanceName":"1"}),"instanceName":"1"}),"instanceName":"1"}),"instanceName":"1"});
            var Q773;
            Q773=makeQuery(id+"F12.opPattern","COPY",BODY,{"derivedFrom":makeQuery(id+"F5.opPattern","COPY",BODY,{"derivedFrom":makeQuery(id+"F1.opRevolve","SWEPT_BODY",BODY,{"disambiguationData":[OSD([sQuery(id+"F0.wireOp",EDGE,"E1")])]}),"instanceName":"1"}),"instanceName":"1"});
            var Q774;
            Q774=makeQuery(id+"F12.opPattern","COPY",BODY,{"derivedFrom":makeQuery(id+"F5.opPattern","COPY",BODY,{"derivedFrom":makeQuery(id+"F2.opPattern","COPY",BODY,{"derivedFrom":makeQuery(id+"F1.opRevolve","SWEPT_BODY",BODY,{"disambiguationData":[OSD([sQuery(id+"F0.wireOp",EDGE,"E1")])]}),"instanceName":"1"}),"instanceName":"1"}),"instanceName":"1"});
            var Q775;
            Q775=makeQuery(id+"F12.opPattern","COPY",BODY,{"derivedFrom":makeQuery(id+"F5.opPattern","COPY",BODY,{"derivedFrom":makeQuery(id+"F3.opPattern","COPY",BODY,{"derivedFrom":makeQuery(id+"F2.opPattern","COPY",BODY,{"derivedFrom":makeQuery(id+"F1.opRevolve","SWEPT_BODY",BODY,{"disambiguationData":[OSD([sQuery(id+"F0.wireOp",EDGE,"E1")])]}),"instanceName":"1"}),"instanceName":"1"}),"instanceName":"1"}),"instanceName":"1"});
            var Q776;
            Q776=makeQuery(id+"F12.opPattern","COPY",BODY,{"derivedFrom":makeQuery(id+"F5.opPattern","COPY",BODY,{"derivedFrom":makeQuery(id+"F4.opPattern","COPY",BODY,{"derivedFrom":makeQuery(id+"F1.opRevolve","SWEPT_BODY",BODY,{"disambiguationData":[OSD([sQuery(id+"F0.wireOp",EDGE,"E1")])]}),"instanceName":"1"}),"instanceName":"1"}),"instanceName":"1"});
            var Q777;
            Q777=makeQuery(id+"F12.opPattern","COPY",BODY,{"derivedFrom":makeQuery(id+"F5.opPattern","COPY",BODY,{"derivedFrom":makeQuery(id+"F4.opPattern","COPY",BODY,{"derivedFrom":makeQuery(id+"F2.opPattern","COPY",BODY,{"derivedFrom":makeQuery(id+"F1.opRevolve","SWEPT_BODY",BODY,{"disambiguationData":[OSD([sQuery(id+"F0.wireOp",EDGE,"E1")])]}),"instanceName":"1"}),"instanceName":"1"}),"instanceName":"1"}),"instanceName":"1"});
            var Q778;
            Q778=makeQuery(id+"F12.opPattern","COPY",BODY,{"derivedFrom":makeQuery(id+"F5.opPattern","COPY",BODY,{"derivedFrom":makeQuery(id+"F4.opPattern","COPY",BODY,{"derivedFrom":makeQuery(id+"F3.opPattern","COPY",BODY,{"derivedFrom":makeQuery(id+"F2.opPattern","COPY",BODY,{"derivedFrom":makeQuery(id+"F1.opRevolve","SWEPT_BODY",BODY,{"disambiguationData":[OSD([sQuery(id+"F0.wireOp",EDGE,"E1")])]}),"instanceName":"1"}),"instanceName":"1"}),"instanceName":"1"}),"instanceName":"1"}),"instanceName":"1"});
            var Q779;
            Q779=makeQuery(id+"F12.opPattern","COPY",BODY,{"derivedFrom":makeQuery(id+"F6.opPattern","COPY",BODY,{"derivedFrom":makeQuery(id+"F1.opRevolve","SWEPT_BODY",BODY,{"disambiguationData":[OSD([sQuery(id+"F0.wireOp",EDGE,"E1")])]}),"instanceName":"1"}),"instanceName":"1"});
            var Q780;
            Q780=makeQuery(id+"F12.opPattern","COPY",BODY,{"derivedFrom":makeQuery(id+"F6.opPattern","COPY",BODY,{"derivedFrom":makeQuery(id+"F2.opPattern","COPY",BODY,{"derivedFrom":makeQuery(id+"F1.opRevolve","SWEPT_BODY",BODY,{"disambiguationData":[OSD([sQuery(id+"F0.wireOp",EDGE,"E1")])]}),"instanceName":"1"}),"instanceName":"1"}),"instanceName":"1"});
            var Q781;
            Q781=makeQuery(id+"F12.opPattern","COPY",BODY,{"derivedFrom":makeQuery(id+"F6.opPattern","COPY",BODY,{"derivedFrom":makeQuery(id+"F3.opPattern","COPY",BODY,{"derivedFrom":makeQuery(id+"F2.opPattern","COPY",BODY,{"derivedFrom":makeQuery(id+"F1.opRevolve","SWEPT_BODY",BODY,{"disambiguationData":[OSD([sQuery(id+"F0.wireOp",EDGE,"E1")])]}),"instanceName":"1"}),"instanceName":"1"}),"instanceName":"1"}),"instanceName":"1"});
            var Q782;
            Q782=makeQuery(id+"F12.opPattern","COPY",BODY,{"derivedFrom":makeQuery(id+"F6.opPattern","COPY",BODY,{"derivedFrom":makeQuery(id+"F4.opPattern","COPY",BODY,{"derivedFrom":makeQuery(id+"F1.opRevolve","SWEPT_BODY",BODY,{"disambiguationData":[OSD([sQuery(id+"F0.wireOp",EDGE,"E1")])]}),"instanceName":"1"}),"instanceName":"1"}),"instanceName":"1"});
            var Q783;
            Q783=makeQuery(id+"F12.opPattern","COPY",BODY,{"derivedFrom":makeQuery(id+"F6.opPattern","COPY",BODY,{"derivedFrom":makeQuery(id+"F4.opPattern","COPY",BODY,{"derivedFrom":makeQuery(id+"F2.opPattern","COPY",BODY,{"derivedFrom":makeQuery(id+"F1.opRevolve","SWEPT_BODY",BODY,{"disambiguationData":[OSD([sQuery(id+"F0.wireOp",EDGE,"E1")])]}),"instanceName":"1"}),"instanceName":"1"}),"instanceName":"1"}),"instanceName":"1"});
            var Q784;
            Q784=makeQuery(id+"F12.opPattern","COPY",BODY,{"derivedFrom":makeQuery(id+"F6.opPattern","COPY",BODY,{"derivedFrom":makeQuery(id+"F4.opPattern","COPY",BODY,{"derivedFrom":makeQuery(id+"F3.opPattern","COPY",BODY,{"derivedFrom":makeQuery(id+"F2.opPattern","COPY",BODY,{"derivedFrom":makeQuery(id+"F1.opRevolve","SWEPT_BODY",BODY,{"disambiguationData":[OSD([sQuery(id+"F0.wireOp",EDGE,"E1")])]}),"instanceName":"1"}),"instanceName":"1"}),"instanceName":"1"}),"instanceName":"1"}),"instanceName":"1"});
            var Q785;
            Q785=makeQuery(id+"F12.opPattern","COPY",BODY,{"derivedFrom":makeQuery(id+"F6.opPattern","COPY",BODY,{"derivedFrom":makeQuery(id+"F5.opPattern","COPY",BODY,{"derivedFrom":makeQuery(id+"F1.opRevolve","SWEPT_BODY",BODY,{"disambiguationData":[OSD([sQuery(id+"F0.wireOp",EDGE,"E1")])]}),"instanceName":"1"}),"instanceName":"1"}),"instanceName":"1"});
            var Q786;
            Q786=makeQuery(id+"F12.opPattern","COPY",BODY,{"derivedFrom":makeQuery(id+"F6.opPattern","COPY",BODY,{"derivedFrom":makeQuery(id+"F5.opPattern","COPY",BODY,{"derivedFrom":makeQuery(id+"F2.opPattern","COPY",BODY,{"derivedFrom":makeQuery(id+"F1.opRevolve","SWEPT_BODY",BODY,{"disambiguationData":[OSD([sQuery(id+"F0.wireOp",EDGE,"E1")])]}),"instanceName":"1"}),"instanceName":"1"}),"instanceName":"1"}),"instanceName":"1"});
            var Q787;
            Q787=makeQuery(id+"F12.opPattern","COPY",BODY,{"derivedFrom":makeQuery(id+"F6.opPattern","COPY",BODY,{"derivedFrom":makeQuery(id+"F5.opPattern","COPY",BODY,{"derivedFrom":makeQuery(id+"F3.opPattern","COPY",BODY,{"derivedFrom":makeQuery(id+"F2.opPattern","COPY",BODY,{"derivedFrom":makeQuery(id+"F1.opRevolve","SWEPT_BODY",BODY,{"disambiguationData":[OSD([sQuery(id+"F0.wireOp",EDGE,"E1")])]}),"instanceName":"1"}),"instanceName":"1"}),"instanceName":"1"}),"instanceName":"1"}),"instanceName":"1"});
            var Q788;
            Q788=makeQuery(id+"F12.opPattern","COPY",BODY,{"derivedFrom":makeQuery(id+"F6.opPattern","COPY",BODY,{"derivedFrom":makeQuery(id+"F5.opPattern","COPY",BODY,{"derivedFrom":makeQuery(id+"F4.opPattern","COPY",BODY,{"derivedFrom":makeQuery(id+"F1.opRevolve","SWEPT_BODY",BODY,{"disambiguationData":[OSD([sQuery(id+"F0.wireOp",EDGE,"E1")])]}),"instanceName":"1"}),"instanceName":"1"}),"instanceName":"1"}),"instanceName":"1"});
            var Q789;
            Q789=makeQuery(id+"F12.opPattern","COPY",BODY,{"derivedFrom":makeQuery(id+"F6.opPattern","COPY",BODY,{"derivedFrom":makeQuery(id+"F5.opPattern","COPY",BODY,{"derivedFrom":makeQuery(id+"F4.opPattern","COPY",BODY,{"derivedFrom":makeQuery(id+"F2.opPattern","COPY",BODY,{"derivedFrom":makeQuery(id+"F1.opRevolve","SWEPT_BODY",BODY,{"disambiguationData":[OSD([sQuery(id+"F0.wireOp",EDGE,"E1")])]}),"instanceName":"1"}),"instanceName":"1"}),"instanceName":"1"}),"instanceName":"1"}),"instanceName":"1"});
            var Q790;
            Q790=makeQuery(id+"F12.opPattern","COPY",BODY,{"derivedFrom":makeQuery(id+"F6.opPattern","COPY",BODY,{"derivedFrom":makeQuery(id+"F5.opPattern","COPY",BODY,{"derivedFrom":makeQuery(id+"F4.opPattern","COPY",BODY,{"derivedFrom":makeQuery(id+"F3.opPattern","COPY",BODY,{"derivedFrom":makeQuery(id+"F2.opPattern","COPY",BODY,{"derivedFrom":makeQuery(id+"F1.opRevolve","SWEPT_BODY",BODY,{"disambiguationData":[OSD([sQuery(id+"F0.wireOp",EDGE,"E1")])]}),"instanceName":"1"}),"instanceName":"1"}),"instanceName":"1"}),"instanceName":"1"}),"instanceName":"1"}),"instanceName":"1"});
            var Q791;
            Q791=makeQuery(id+"F12.opPattern","COPY",BODY,{"derivedFrom":makeQuery(id+"F7.opPattern","COPY",BODY,{"derivedFrom":makeQuery(id+"F1.opRevolve","SWEPT_BODY",BODY,{"disambiguationData":[OSD([sQuery(id+"F0.wireOp",EDGE,"E1")])]}),"instanceName":"1"}),"instanceName":"1"});
            var Q792;
            Q792=makeQuery(id+"F12.opPattern","COPY",BODY,{"derivedFrom":makeQuery(id+"F7.opPattern","COPY",BODY,{"derivedFrom":makeQuery(id+"F2.opPattern","COPY",BODY,{"derivedFrom":makeQuery(id+"F1.opRevolve","SWEPT_BODY",BODY,{"disambiguationData":[OSD([sQuery(id+"F0.wireOp",EDGE,"E1")])]}),"instanceName":"1"}),"instanceName":"1"}),"instanceName":"1"});
            var Q793;
            Q793=makeQuery(id+"F12.opPattern","COPY",BODY,{"derivedFrom":makeQuery(id+"F7.opPattern","COPY",BODY,{"derivedFrom":makeQuery(id+"F3.opPattern","COPY",BODY,{"derivedFrom":makeQuery(id+"F2.opPattern","COPY",BODY,{"derivedFrom":makeQuery(id+"F1.opRevolve","SWEPT_BODY",BODY,{"disambiguationData":[OSD([sQuery(id+"F0.wireOp",EDGE,"E1")])]}),"instanceName":"1"}),"instanceName":"1"}),"instanceName":"1"}),"instanceName":"1"});
            var Q794;
            Q794=makeQuery(id+"F12.opPattern","COPY",BODY,{"derivedFrom":makeQuery(id+"F7.opPattern","COPY",BODY,{"derivedFrom":makeQuery(id+"F4.opPattern","COPY",BODY,{"derivedFrom":makeQuery(id+"F1.opRevolve","SWEPT_BODY",BODY,{"disambiguationData":[OSD([sQuery(id+"F0.wireOp",EDGE,"E1")])]}),"instanceName":"1"}),"instanceName":"1"}),"instanceName":"1"});
            var Q795;
            Q795=makeQuery(id+"F12.opPattern","COPY",BODY,{"derivedFrom":makeQuery(id+"F7.opPattern","COPY",BODY,{"derivedFrom":makeQuery(id+"F4.opPattern","COPY",BODY,{"derivedFrom":makeQuery(id+"F2.opPattern","COPY",BODY,{"derivedFrom":makeQuery(id+"F1.opRevolve","SWEPT_BODY",BODY,{"disambiguationData":[OSD([sQuery(id+"F0.wireOp",EDGE,"E1")])]}),"instanceName":"1"}),"instanceName":"1"}),"instanceName":"1"}),"instanceName":"1"});
            var Q796;
            Q796=makeQuery(id+"F12.opPattern","COPY",BODY,{"derivedFrom":makeQuery(id+"F7.opPattern","COPY",BODY,{"derivedFrom":makeQuery(id+"F4.opPattern","COPY",BODY,{"derivedFrom":makeQuery(id+"F3.opPattern","COPY",BODY,{"derivedFrom":makeQuery(id+"F2.opPattern","COPY",BODY,{"derivedFrom":makeQuery(id+"F1.opRevolve","SWEPT_BODY",BODY,{"disambiguationData":[OSD([sQuery(id+"F0.wireOp",EDGE,"E1")])]}),"instanceName":"1"}),"instanceName":"1"}),"instanceName":"1"}),"instanceName":"1"}),"instanceName":"1"});
            var Q797;
            Q797=makeQuery(id+"F12.opPattern","COPY",BODY,{"derivedFrom":makeQuery(id+"F7.opPattern","COPY",BODY,{"derivedFrom":makeQuery(id+"F5.opPattern","COPY",BODY,{"derivedFrom":makeQuery(id+"F1.opRevolve","SWEPT_BODY",BODY,{"disambiguationData":[OSD([sQuery(id+"F0.wireOp",EDGE,"E1")])]}),"instanceName":"1"}),"instanceName":"1"}),"instanceName":"1"});
            var Q798;
            Q798=makeQuery(id+"F12.opPattern","COPY",BODY,{"derivedFrom":makeQuery(id+"F7.opPattern","COPY",BODY,{"derivedFrom":makeQuery(id+"F5.opPattern","COPY",BODY,{"derivedFrom":makeQuery(id+"F2.opPattern","COPY",BODY,{"derivedFrom":makeQuery(id+"F1.opRevolve","SWEPT_BODY",BODY,{"disambiguationData":[OSD([sQuery(id+"F0.wireOp",EDGE,"E1")])]}),"instanceName":"1"}),"instanceName":"1"}),"instanceName":"1"}),"instanceName":"1"});
            var Q799;
            Q799=makeQuery(id+"F12.opPattern","COPY",BODY,{"derivedFrom":makeQuery(id+"F7.opPattern","COPY",BODY,{"derivedFrom":makeQuery(id+"F5.opPattern","COPY",BODY,{"derivedFrom":makeQuery(id+"F3.opPattern","COPY",BODY,{"derivedFrom":makeQuery(id+"F2.opPattern","COPY",BODY,{"derivedFrom":makeQuery(id+"F1.opRevolve","SWEPT_BODY",BODY,{"disambiguationData":[OSD([sQuery(id+"F0.wireOp",EDGE,"E1")])]}),"instanceName":"1"}),"instanceName":"1"}),"instanceName":"1"}),"instanceName":"1"}),"instanceName":"1"});
            var Q800;
            Q800=makeQuery(id+"F12.opPattern","COPY",BODY,{"derivedFrom":makeQuery(id+"F7.opPattern","COPY",BODY,{"derivedFrom":makeQuery(id+"F5.opPattern","COPY",BODY,{"derivedFrom":makeQuery(id+"F4.opPattern","COPY",BODY,{"derivedFrom":makeQuery(id+"F1.opRevolve","SWEPT_BODY",BODY,{"disambiguationData":[OSD([sQuery(id+"F0.wireOp",EDGE,"E1")])]}),"instanceName":"1"}),"instanceName":"1"}),"instanceName":"1"}),"instanceName":"1"});
            var Q801;
            Q801=makeQuery(id+"F12.opPattern","COPY",BODY,{"derivedFrom":makeQuery(id+"F7.opPattern","COPY",BODY,{"derivedFrom":makeQuery(id+"F5.opPattern","COPY",BODY,{"derivedFrom":makeQuery(id+"F4.opPattern","COPY",BODY,{"derivedFrom":makeQuery(id+"F2.opPattern","COPY",BODY,{"derivedFrom":makeQuery(id+"F1.opRevolve","SWEPT_BODY",BODY,{"disambiguationData":[OSD([sQuery(id+"F0.wireOp",EDGE,"E1")])]}),"instanceName":"1"}),"instanceName":"1"}),"instanceName":"1"}),"instanceName":"1"}),"instanceName":"1"});
            var Q802;
            Q802=makeQuery(id+"F12.opPattern","COPY",BODY,{"derivedFrom":makeQuery(id+"F7.opPattern","COPY",BODY,{"derivedFrom":makeQuery(id+"F5.opPattern","COPY",BODY,{"derivedFrom":makeQuery(id+"F4.opPattern","COPY",BODY,{"derivedFrom":makeQuery(id+"F3.opPattern","COPY",BODY,{"derivedFrom":makeQuery(id+"F2.opPattern","COPY",BODY,{"derivedFrom":makeQuery(id+"F1.opRevolve","SWEPT_BODY",BODY,{"disambiguationData":[OSD([sQuery(id+"F0.wireOp",EDGE,"E1")])]}),"instanceName":"1"}),"instanceName":"1"}),"instanceName":"1"}),"instanceName":"1"}),"instanceName":"1"}),"instanceName":"1"});
            var Q803;
            Q803=makeQuery(id+"F12.opPattern","COPY",BODY,{"derivedFrom":makeQuery(id+"F7.opPattern","COPY",BODY,{"derivedFrom":makeQuery(id+"F6.opPattern","COPY",BODY,{"derivedFrom":makeQuery(id+"F1.opRevolve","SWEPT_BODY",BODY,{"disambiguationData":[OSD([sQuery(id+"F0.wireOp",EDGE,"E1")])]}),"instanceName":"1"}),"instanceName":"1"}),"instanceName":"1"});
            var Q804;
            Q804=makeQuery(id+"F12.opPattern","COPY",BODY,{"derivedFrom":makeQuery(id+"F7.opPattern","COPY",BODY,{"derivedFrom":makeQuery(id+"F6.opPattern","COPY",BODY,{"derivedFrom":makeQuery(id+"F2.opPattern","COPY",BODY,{"derivedFrom":makeQuery(id+"F1.opRevolve","SWEPT_BODY",BODY,{"disambiguationData":[OSD([sQuery(id+"F0.wireOp",EDGE,"E1")])]}),"instanceName":"1"}),"instanceName":"1"}),"instanceName":"1"}),"instanceName":"1"});
            var Q805;
            Q805=makeQuery(id+"F12.opPattern","COPY",BODY,{"derivedFrom":makeQuery(id+"F7.opPattern","COPY",BODY,{"derivedFrom":makeQuery(id+"F6.opPattern","COPY",BODY,{"derivedFrom":makeQuery(id+"F3.opPattern","COPY",BODY,{"derivedFrom":makeQuery(id+"F2.opPattern","COPY",BODY,{"derivedFrom":makeQuery(id+"F1.opRevolve","SWEPT_BODY",BODY,{"disambiguationData":[OSD([sQuery(id+"F0.wireOp",EDGE,"E1")])]}),"instanceName":"1"}),"instanceName":"1"}),"instanceName":"1"}),"instanceName":"1"}),"instanceName":"1"});
            var Q806;
            Q806=makeQuery(id+"F12.opPattern","COPY",BODY,{"derivedFrom":makeQuery(id+"F7.opPattern","COPY",BODY,{"derivedFrom":makeQuery(id+"F6.opPattern","COPY",BODY,{"derivedFrom":makeQuery(id+"F4.opPattern","COPY",BODY,{"derivedFrom":makeQuery(id+"F1.opRevolve","SWEPT_BODY",BODY,{"disambiguationData":[OSD([sQuery(id+"F0.wireOp",EDGE,"E1")])]}),"instanceName":"1"}),"instanceName":"1"}),"instanceName":"1"}),"instanceName":"1"});
            var Q807;
            Q807=makeQuery(id+"F12.opPattern","COPY",BODY,{"derivedFrom":makeQuery(id+"F7.opPattern","COPY",BODY,{"derivedFrom":makeQuery(id+"F6.opPattern","COPY",BODY,{"derivedFrom":makeQuery(id+"F4.opPattern","COPY",BODY,{"derivedFrom":makeQuery(id+"F2.opPattern","COPY",BODY,{"derivedFrom":makeQuery(id+"F1.opRevolve","SWEPT_BODY",BODY,{"disambiguationData":[OSD([sQuery(id+"F0.wireOp",EDGE,"E1")])]}),"instanceName":"1"}),"instanceName":"1"}),"instanceName":"1"}),"instanceName":"1"}),"instanceName":"1"});
            var Q808;
            Q808=makeQuery(id+"F12.opPattern","COPY",BODY,{"derivedFrom":makeQuery(id+"F7.opPattern","COPY",BODY,{"derivedFrom":makeQuery(id+"F6.opPattern","COPY",BODY,{"derivedFrom":makeQuery(id+"F4.opPattern","COPY",BODY,{"derivedFrom":makeQuery(id+"F3.opPattern","COPY",BODY,{"derivedFrom":makeQuery(id+"F2.opPattern","COPY",BODY,{"derivedFrom":makeQuery(id+"F1.opRevolve","SWEPT_BODY",BODY,{"disambiguationData":[OSD([sQuery(id+"F0.wireOp",EDGE,"E1")])]}),"instanceName":"1"}),"instanceName":"1"}),"instanceName":"1"}),"instanceName":"1"}),"instanceName":"1"}),"instanceName":"1"});
            var Q809;
            Q809=makeQuery(id+"F12.opPattern","COPY",BODY,{"derivedFrom":makeQuery(id+"F7.opPattern","COPY",BODY,{"derivedFrom":makeQuery(id+"F6.opPattern","COPY",BODY,{"derivedFrom":makeQuery(id+"F5.opPattern","COPY",BODY,{"derivedFrom":makeQuery(id+"F1.opRevolve","SWEPT_BODY",BODY,{"disambiguationData":[OSD([sQuery(id+"F0.wireOp",EDGE,"E1")])]}),"instanceName":"1"}),"instanceName":"1"}),"instanceName":"1"}),"instanceName":"1"});
            var Q810;
            Q810=makeQuery(id+"F12.opPattern","COPY",BODY,{"derivedFrom":makeQuery(id+"F7.opPattern","COPY",BODY,{"derivedFrom":makeQuery(id+"F6.opPattern","COPY",BODY,{"derivedFrom":makeQuery(id+"F5.opPattern","COPY",BODY,{"derivedFrom":makeQuery(id+"F2.opPattern","COPY",BODY,{"derivedFrom":makeQuery(id+"F1.opRevolve","SWEPT_BODY",BODY,{"disambiguationData":[OSD([sQuery(id+"F0.wireOp",EDGE,"E1")])]}),"instanceName":"1"}),"instanceName":"1"}),"instanceName":"1"}),"instanceName":"1"}),"instanceName":"1"});
            var Q811;
            Q811=makeQuery(id+"F12.opPattern","COPY",BODY,{"derivedFrom":makeQuery(id+"F7.opPattern","COPY",BODY,{"derivedFrom":makeQuery(id+"F6.opPattern","COPY",BODY,{"derivedFrom":makeQuery(id+"F5.opPattern","COPY",BODY,{"derivedFrom":makeQuery(id+"F3.opPattern","COPY",BODY,{"derivedFrom":makeQuery(id+"F2.opPattern","COPY",BODY,{"derivedFrom":makeQuery(id+"F1.opRevolve","SWEPT_BODY",BODY,{"disambiguationData":[OSD([sQuery(id+"F0.wireOp",EDGE,"E1")])]}),"instanceName":"1"}),"instanceName":"1"}),"instanceName":"1"}),"instanceName":"1"}),"instanceName":"1"}),"instanceName":"1"});
            var Q812;
            Q812=makeQuery(id+"F12.opPattern","COPY",BODY,{"derivedFrom":makeQuery(id+"F7.opPattern","COPY",BODY,{"derivedFrom":makeQuery(id+"F6.opPattern","COPY",BODY,{"derivedFrom":makeQuery(id+"F5.opPattern","COPY",BODY,{"derivedFrom":makeQuery(id+"F4.opPattern","COPY",BODY,{"derivedFrom":makeQuery(id+"F1.opRevolve","SWEPT_BODY",BODY,{"disambiguationData":[OSD([sQuery(id+"F0.wireOp",EDGE,"E1")])]}),"instanceName":"1"}),"instanceName":"1"}),"instanceName":"1"}),"instanceName":"1"}),"instanceName":"1"});
            var Q813;
            Q813=makeQuery(id+"F12.opPattern","COPY",BODY,{"derivedFrom":makeQuery(id+"F7.opPattern","COPY",BODY,{"derivedFrom":makeQuery(id+"F6.opPattern","COPY",BODY,{"derivedFrom":makeQuery(id+"F5.opPattern","COPY",BODY,{"derivedFrom":makeQuery(id+"F4.opPattern","COPY",BODY,{"derivedFrom":makeQuery(id+"F2.opPattern","COPY",BODY,{"derivedFrom":makeQuery(id+"F1.opRevolve","SWEPT_BODY",BODY,{"disambiguationData":[OSD([sQuery(id+"F0.wireOp",EDGE,"E1")])]}),"instanceName":"1"}),"instanceName":"1"}),"instanceName":"1"}),"instanceName":"1"}),"instanceName":"1"}),"instanceName":"1"});
            var Q814;
            Q814=makeQuery(id+"F12.opPattern","COPY",BODY,{"derivedFrom":makeQuery(id+"F7.opPattern","COPY",BODY,{"derivedFrom":makeQuery(id+"F6.opPattern","COPY",BODY,{"derivedFrom":makeQuery(id+"F5.opPattern","COPY",BODY,{"derivedFrom":makeQuery(id+"F4.opPattern","COPY",BODY,{"derivedFrom":makeQuery(id+"F3.opPattern","COPY",BODY,{"derivedFrom":makeQuery(id+"F2.opPattern","COPY",BODY,{"derivedFrom":makeQuery(id+"F1.opRevolve","SWEPT_BODY",BODY,{"disambiguationData":[OSD([sQuery(id+"F0.wireOp",EDGE,"E1")])]}),"instanceName":"1"}),"instanceName":"1"}),"instanceName":"1"}),"instanceName":"1"}),"instanceName":"1"}),"instanceName":"1"}),"instanceName":"1"});
            var Q815;
            Q815=makeQuery(id+"F12.opPattern","COPY",BODY,{"derivedFrom":makeQuery(id+"F8.opPattern","COPY",BODY,{"derivedFrom":makeQuery(id+"F1.opRevolve","SWEPT_BODY",BODY,{"disambiguationData":[OSD([sQuery(id+"F0.wireOp",EDGE,"E1")])]}),"instanceName":"1"}),"instanceName":"1"});
            var Q816;
            Q816=makeQuery(id+"F12.opPattern","COPY",BODY,{"derivedFrom":makeQuery(id+"F8.opPattern","COPY",BODY,{"derivedFrom":makeQuery(id+"F2.opPattern","COPY",BODY,{"derivedFrom":makeQuery(id+"F1.opRevolve","SWEPT_BODY",BODY,{"disambiguationData":[OSD([sQuery(id+"F0.wireOp",EDGE,"E1")])]}),"instanceName":"1"}),"instanceName":"1"}),"instanceName":"1"});
            var Q817;
            Q817=makeQuery(id+"F12.opPattern","COPY",BODY,{"derivedFrom":makeQuery(id+"F8.opPattern","COPY",BODY,{"derivedFrom":makeQuery(id+"F3.opPattern","COPY",BODY,{"derivedFrom":makeQuery(id+"F2.opPattern","COPY",BODY,{"derivedFrom":makeQuery(id+"F1.opRevolve","SWEPT_BODY",BODY,{"disambiguationData":[OSD([sQuery(id+"F0.wireOp",EDGE,"E1")])]}),"instanceName":"1"}),"instanceName":"1"}),"instanceName":"1"}),"instanceName":"1"});
            var Q818;
            Q818=makeQuery(id+"F12.opPattern","COPY",BODY,{"derivedFrom":makeQuery(id+"F8.opPattern","COPY",BODY,{"derivedFrom":makeQuery(id+"F4.opPattern","COPY",BODY,{"derivedFrom":makeQuery(id+"F1.opRevolve","SWEPT_BODY",BODY,{"disambiguationData":[OSD([sQuery(id+"F0.wireOp",EDGE,"E1")])]}),"instanceName":"1"}),"instanceName":"1"}),"instanceName":"1"});
            var Q819;
            Q819=makeQuery(id+"F12.opPattern","COPY",BODY,{"derivedFrom":makeQuery(id+"F8.opPattern","COPY",BODY,{"derivedFrom":makeQuery(id+"F4.opPattern","COPY",BODY,{"derivedFrom":makeQuery(id+"F2.opPattern","COPY",BODY,{"derivedFrom":makeQuery(id+"F1.opRevolve","SWEPT_BODY",BODY,{"disambiguationData":[OSD([sQuery(id+"F0.wireOp",EDGE,"E1")])]}),"instanceName":"1"}),"instanceName":"1"}),"instanceName":"1"}),"instanceName":"1"});
            var Q820;
            Q820=makeQuery(id+"F12.opPattern","COPY",BODY,{"derivedFrom":makeQuery(id+"F8.opPattern","COPY",BODY,{"derivedFrom":makeQuery(id+"F4.opPattern","COPY",BODY,{"derivedFrom":makeQuery(id+"F3.opPattern","COPY",BODY,{"derivedFrom":makeQuery(id+"F2.opPattern","COPY",BODY,{"derivedFrom":makeQuery(id+"F1.opRevolve","SWEPT_BODY",BODY,{"disambiguationData":[OSD([sQuery(id+"F0.wireOp",EDGE,"E1")])]}),"instanceName":"1"}),"instanceName":"1"}),"instanceName":"1"}),"instanceName":"1"}),"instanceName":"1"});
            var Q821;
            Q821=makeQuery(id+"F12.opPattern","COPY",BODY,{"derivedFrom":makeQuery(id+"F8.opPattern","COPY",BODY,{"derivedFrom":makeQuery(id+"F5.opPattern","COPY",BODY,{"derivedFrom":makeQuery(id+"F1.opRevolve","SWEPT_BODY",BODY,{"disambiguationData":[OSD([sQuery(id+"F0.wireOp",EDGE,"E1")])]}),"instanceName":"1"}),"instanceName":"1"}),"instanceName":"1"});
            var Q822;
            Q822=makeQuery(id+"F12.opPattern","COPY",BODY,{"derivedFrom":makeQuery(id+"F8.opPattern","COPY",BODY,{"derivedFrom":makeQuery(id+"F5.opPattern","COPY",BODY,{"derivedFrom":makeQuery(id+"F2.opPattern","COPY",BODY,{"derivedFrom":makeQuery(id+"F1.opRevolve","SWEPT_BODY",BODY,{"disambiguationData":[OSD([sQuery(id+"F0.wireOp",EDGE,"E1")])]}),"instanceName":"1"}),"instanceName":"1"}),"instanceName":"1"}),"instanceName":"1"});
            var Q823;
            Q823=makeQuery(id+"F12.opPattern","COPY",BODY,{"derivedFrom":makeQuery(id+"F8.opPattern","COPY",BODY,{"derivedFrom":makeQuery(id+"F5.opPattern","COPY",BODY,{"derivedFrom":makeQuery(id+"F3.opPattern","COPY",BODY,{"derivedFrom":makeQuery(id+"F2.opPattern","COPY",BODY,{"derivedFrom":makeQuery(id+"F1.opRevolve","SWEPT_BODY",BODY,{"disambiguationData":[OSD([sQuery(id+"F0.wireOp",EDGE,"E1")])]}),"instanceName":"1"}),"instanceName":"1"}),"instanceName":"1"}),"instanceName":"1"}),"instanceName":"1"});
            var Q824;
            Q824=makeQuery(id+"F12.opPattern","COPY",BODY,{"derivedFrom":makeQuery(id+"F8.opPattern","COPY",BODY,{"derivedFrom":makeQuery(id+"F5.opPattern","COPY",BODY,{"derivedFrom":makeQuery(id+"F4.opPattern","COPY",BODY,{"derivedFrom":makeQuery(id+"F1.opRevolve","SWEPT_BODY",BODY,{"disambiguationData":[OSD([sQuery(id+"F0.wireOp",EDGE,"E1")])]}),"instanceName":"1"}),"instanceName":"1"}),"instanceName":"1"}),"instanceName":"1"});
            var Q825;
            Q825=makeQuery(id+"F12.opPattern","COPY",BODY,{"derivedFrom":makeQuery(id+"F8.opPattern","COPY",BODY,{"derivedFrom":makeQuery(id+"F5.opPattern","COPY",BODY,{"derivedFrom":makeQuery(id+"F4.opPattern","COPY",BODY,{"derivedFrom":makeQuery(id+"F2.opPattern","COPY",BODY,{"derivedFrom":makeQuery(id+"F1.opRevolve","SWEPT_BODY",BODY,{"disambiguationData":[OSD([sQuery(id+"F0.wireOp",EDGE,"E1")])]}),"instanceName":"1"}),"instanceName":"1"}),"instanceName":"1"}),"instanceName":"1"}),"instanceName":"1"});
            var Q826;
            Q826=makeQuery(id+"F12.opPattern","COPY",BODY,{"derivedFrom":makeQuery(id+"F8.opPattern","COPY",BODY,{"derivedFrom":makeQuery(id+"F5.opPattern","COPY",BODY,{"derivedFrom":makeQuery(id+"F4.opPattern","COPY",BODY,{"derivedFrom":makeQuery(id+"F3.opPattern","COPY",BODY,{"derivedFrom":makeQuery(id+"F2.opPattern","COPY",BODY,{"derivedFrom":makeQuery(id+"F1.opRevolve","SWEPT_BODY",BODY,{"disambiguationData":[OSD([sQuery(id+"F0.wireOp",EDGE,"E1")])]}),"instanceName":"1"}),"instanceName":"1"}),"instanceName":"1"}),"instanceName":"1"}),"instanceName":"1"}),"instanceName":"1"});
            var Q827;
            Q827=makeQuery(id+"F12.opPattern","COPY",BODY,{"derivedFrom":makeQuery(id+"F8.opPattern","COPY",BODY,{"derivedFrom":makeQuery(id+"F6.opPattern","COPY",BODY,{"derivedFrom":makeQuery(id+"F1.opRevolve","SWEPT_BODY",BODY,{"disambiguationData":[OSD([sQuery(id+"F0.wireOp",EDGE,"E1")])]}),"instanceName":"1"}),"instanceName":"1"}),"instanceName":"1"});
            var Q828;
            Q828=makeQuery(id+"F12.opPattern","COPY",BODY,{"derivedFrom":makeQuery(id+"F8.opPattern","COPY",BODY,{"derivedFrom":makeQuery(id+"F6.opPattern","COPY",BODY,{"derivedFrom":makeQuery(id+"F2.opPattern","COPY",BODY,{"derivedFrom":makeQuery(id+"F1.opRevolve","SWEPT_BODY",BODY,{"disambiguationData":[OSD([sQuery(id+"F0.wireOp",EDGE,"E1")])]}),"instanceName":"1"}),"instanceName":"1"}),"instanceName":"1"}),"instanceName":"1"});
            var Q829;
            Q829=makeQuery(id+"F12.opPattern","COPY",BODY,{"derivedFrom":makeQuery(id+"F8.opPattern","COPY",BODY,{"derivedFrom":makeQuery(id+"F6.opPattern","COPY",BODY,{"derivedFrom":makeQuery(id+"F3.opPattern","COPY",BODY,{"derivedFrom":makeQuery(id+"F2.opPattern","COPY",BODY,{"derivedFrom":makeQuery(id+"F1.opRevolve","SWEPT_BODY",BODY,{"disambiguationData":[OSD([sQuery(id+"F0.wireOp",EDGE,"E1")])]}),"instanceName":"1"}),"instanceName":"1"}),"instanceName":"1"}),"instanceName":"1"}),"instanceName":"1"});
            var Q830;
            Q830=makeQuery(id+"F12.opPattern","COPY",BODY,{"derivedFrom":makeQuery(id+"F8.opPattern","COPY",BODY,{"derivedFrom":makeQuery(id+"F6.opPattern","COPY",BODY,{"derivedFrom":makeQuery(id+"F4.opPattern","COPY",BODY,{"derivedFrom":makeQuery(id+"F1.opRevolve","SWEPT_BODY",BODY,{"disambiguationData":[OSD([sQuery(id+"F0.wireOp",EDGE,"E1")])]}),"instanceName":"1"}),"instanceName":"1"}),"instanceName":"1"}),"instanceName":"1"});
            var Q831;
            Q831=makeQuery(id+"F12.opPattern","COPY",BODY,{"derivedFrom":makeQuery(id+"F8.opPattern","COPY",BODY,{"derivedFrom":makeQuery(id+"F6.opPattern","COPY",BODY,{"derivedFrom":makeQuery(id+"F4.opPattern","COPY",BODY,{"derivedFrom":makeQuery(id+"F2.opPattern","COPY",BODY,{"derivedFrom":makeQuery(id+"F1.opRevolve","SWEPT_BODY",BODY,{"disambiguationData":[OSD([sQuery(id+"F0.wireOp",EDGE,"E1")])]}),"instanceName":"1"}),"instanceName":"1"}),"instanceName":"1"}),"instanceName":"1"}),"instanceName":"1"});
            var Q832;
            Q832=makeQuery(id+"F12.opPattern","COPY",BODY,{"derivedFrom":makeQuery(id+"F8.opPattern","COPY",BODY,{"derivedFrom":makeQuery(id+"F6.opPattern","COPY",BODY,{"derivedFrom":makeQuery(id+"F4.opPattern","COPY",BODY,{"derivedFrom":makeQuery(id+"F3.opPattern","COPY",BODY,{"derivedFrom":makeQuery(id+"F2.opPattern","COPY",BODY,{"derivedFrom":makeQuery(id+"F1.opRevolve","SWEPT_BODY",BODY,{"disambiguationData":[OSD([sQuery(id+"F0.wireOp",EDGE,"E1")])]}),"instanceName":"1"}),"instanceName":"1"}),"instanceName":"1"}),"instanceName":"1"}),"instanceName":"1"}),"instanceName":"1"});
            var Q833;
            Q833=makeQuery(id+"F12.opPattern","COPY",BODY,{"derivedFrom":makeQuery(id+"F8.opPattern","COPY",BODY,{"derivedFrom":makeQuery(id+"F6.opPattern","COPY",BODY,{"derivedFrom":makeQuery(id+"F5.opPattern","COPY",BODY,{"derivedFrom":makeQuery(id+"F1.opRevolve","SWEPT_BODY",BODY,{"disambiguationData":[OSD([sQuery(id+"F0.wireOp",EDGE,"E1")])]}),"instanceName":"1"}),"instanceName":"1"}),"instanceName":"1"}),"instanceName":"1"});
            var Q834;
            Q834=makeQuery(id+"F12.opPattern","COPY",BODY,{"derivedFrom":makeQuery(id+"F8.opPattern","COPY",BODY,{"derivedFrom":makeQuery(id+"F6.opPattern","COPY",BODY,{"derivedFrom":makeQuery(id+"F5.opPattern","COPY",BODY,{"derivedFrom":makeQuery(id+"F2.opPattern","COPY",BODY,{"derivedFrom":makeQuery(id+"F1.opRevolve","SWEPT_BODY",BODY,{"disambiguationData":[OSD([sQuery(id+"F0.wireOp",EDGE,"E1")])]}),"instanceName":"1"}),"instanceName":"1"}),"instanceName":"1"}),"instanceName":"1"}),"instanceName":"1"});
            var Q835;
            Q835=makeQuery(id+"F12.opPattern","COPY",BODY,{"derivedFrom":makeQuery(id+"F8.opPattern","COPY",BODY,{"derivedFrom":makeQuery(id+"F6.opPattern","COPY",BODY,{"derivedFrom":makeQuery(id+"F5.opPattern","COPY",BODY,{"derivedFrom":makeQuery(id+"F3.opPattern","COPY",BODY,{"derivedFrom":makeQuery(id+"F2.opPattern","COPY",BODY,{"derivedFrom":makeQuery(id+"F1.opRevolve","SWEPT_BODY",BODY,{"disambiguationData":[OSD([sQuery(id+"F0.wireOp",EDGE,"E1")])]}),"instanceName":"1"}),"instanceName":"1"}),"instanceName":"1"}),"instanceName":"1"}),"instanceName":"1"}),"instanceName":"1"});
            var Q836;
            Q836=makeQuery(id+"F12.opPattern","COPY",BODY,{"derivedFrom":makeQuery(id+"F8.opPattern","COPY",BODY,{"derivedFrom":makeQuery(id+"F6.opPattern","COPY",BODY,{"derivedFrom":makeQuery(id+"F5.opPattern","COPY",BODY,{"derivedFrom":makeQuery(id+"F4.opPattern","COPY",BODY,{"derivedFrom":makeQuery(id+"F1.opRevolve","SWEPT_BODY",BODY,{"disambiguationData":[OSD([sQuery(id+"F0.wireOp",EDGE,"E1")])]}),"instanceName":"1"}),"instanceName":"1"}),"instanceName":"1"}),"instanceName":"1"}),"instanceName":"1"});
            var Q837;
            Q837=makeQuery(id+"F12.opPattern","COPY",BODY,{"derivedFrom":makeQuery(id+"F8.opPattern","COPY",BODY,{"derivedFrom":makeQuery(id+"F6.opPattern","COPY",BODY,{"derivedFrom":makeQuery(id+"F5.opPattern","COPY",BODY,{"derivedFrom":makeQuery(id+"F4.opPattern","COPY",BODY,{"derivedFrom":makeQuery(id+"F2.opPattern","COPY",BODY,{"derivedFrom":makeQuery(id+"F1.opRevolve","SWEPT_BODY",BODY,{"disambiguationData":[OSD([sQuery(id+"F0.wireOp",EDGE,"E1")])]}),"instanceName":"1"}),"instanceName":"1"}),"instanceName":"1"}),"instanceName":"1"}),"instanceName":"1"}),"instanceName":"1"});
            var Q838;
            Q838=makeQuery(id+"F12.opPattern","COPY",BODY,{"derivedFrom":makeQuery(id+"F8.opPattern","COPY",BODY,{"derivedFrom":makeQuery(id+"F6.opPattern","COPY",BODY,{"derivedFrom":makeQuery(id+"F5.opPattern","COPY",BODY,{"derivedFrom":makeQuery(id+"F4.opPattern","COPY",BODY,{"derivedFrom":makeQuery(id+"F3.opPattern","COPY",BODY,{"derivedFrom":makeQuery(id+"F2.opPattern","COPY",BODY,{"derivedFrom":makeQuery(id+"F1.opRevolve","SWEPT_BODY",BODY,{"disambiguationData":[OSD([sQuery(id+"F0.wireOp",EDGE,"E1")])]}),"instanceName":"1"}),"instanceName":"1"}),"instanceName":"1"}),"instanceName":"1"}),"instanceName":"1"}),"instanceName":"1"}),"instanceName":"1"});
            var Q839;
            Q839=makeQuery(id+"F12.opPattern","COPY",BODY,{"derivedFrom":makeQuery(id+"F8.opPattern","COPY",BODY,{"derivedFrom":makeQuery(id+"F7.opPattern","COPY",BODY,{"derivedFrom":makeQuery(id+"F1.opRevolve","SWEPT_BODY",BODY,{"disambiguationData":[OSD([sQuery(id+"F0.wireOp",EDGE,"E1")])]}),"instanceName":"1"}),"instanceName":"1"}),"instanceName":"1"});
            var Q840;
            Q840=makeQuery(id+"F12.opPattern","COPY",BODY,{"derivedFrom":makeQuery(id+"F8.opPattern","COPY",BODY,{"derivedFrom":makeQuery(id+"F7.opPattern","COPY",BODY,{"derivedFrom":makeQuery(id+"F2.opPattern","COPY",BODY,{"derivedFrom":makeQuery(id+"F1.opRevolve","SWEPT_BODY",BODY,{"disambiguationData":[OSD([sQuery(id+"F0.wireOp",EDGE,"E1")])]}),"instanceName":"1"}),"instanceName":"1"}),"instanceName":"1"}),"instanceName":"1"});
            var Q841;
            Q841=makeQuery(id+"F12.opPattern","COPY",BODY,{"derivedFrom":makeQuery(id+"F8.opPattern","COPY",BODY,{"derivedFrom":makeQuery(id+"F7.opPattern","COPY",BODY,{"derivedFrom":makeQuery(id+"F3.opPattern","COPY",BODY,{"derivedFrom":makeQuery(id+"F2.opPattern","COPY",BODY,{"derivedFrom":makeQuery(id+"F1.opRevolve","SWEPT_BODY",BODY,{"disambiguationData":[OSD([sQuery(id+"F0.wireOp",EDGE,"E1")])]}),"instanceName":"1"}),"instanceName":"1"}),"instanceName":"1"}),"instanceName":"1"}),"instanceName":"1"});
            var Q842;
            Q842=makeQuery(id+"F12.opPattern","COPY",BODY,{"derivedFrom":makeQuery(id+"F8.opPattern","COPY",BODY,{"derivedFrom":makeQuery(id+"F7.opPattern","COPY",BODY,{"derivedFrom":makeQuery(id+"F4.opPattern","COPY",BODY,{"derivedFrom":makeQuery(id+"F1.opRevolve","SWEPT_BODY",BODY,{"disambiguationData":[OSD([sQuery(id+"F0.wireOp",EDGE,"E1")])]}),"instanceName":"1"}),"instanceName":"1"}),"instanceName":"1"}),"instanceName":"1"});
            var Q843;
            Q843=makeQuery(id+"F12.opPattern","COPY",BODY,{"derivedFrom":makeQuery(id+"F8.opPattern","COPY",BODY,{"derivedFrom":makeQuery(id+"F7.opPattern","COPY",BODY,{"derivedFrom":makeQuery(id+"F4.opPattern","COPY",BODY,{"derivedFrom":makeQuery(id+"F2.opPattern","COPY",BODY,{"derivedFrom":makeQuery(id+"F1.opRevolve","SWEPT_BODY",BODY,{"disambiguationData":[OSD([sQuery(id+"F0.wireOp",EDGE,"E1")])]}),"instanceName":"1"}),"instanceName":"1"}),"instanceName":"1"}),"instanceName":"1"}),"instanceName":"1"});
            var Q844;
            Q844=makeQuery(id+"F12.opPattern","COPY",BODY,{"derivedFrom":makeQuery(id+"F8.opPattern","COPY",BODY,{"derivedFrom":makeQuery(id+"F7.opPattern","COPY",BODY,{"derivedFrom":makeQuery(id+"F4.opPattern","COPY",BODY,{"derivedFrom":makeQuery(id+"F3.opPattern","COPY",BODY,{"derivedFrom":makeQuery(id+"F2.opPattern","COPY",BODY,{"derivedFrom":makeQuery(id+"F1.opRevolve","SWEPT_BODY",BODY,{"disambiguationData":[OSD([sQuery(id+"F0.wireOp",EDGE,"E1")])]}),"instanceName":"1"}),"instanceName":"1"}),"instanceName":"1"}),"instanceName":"1"}),"instanceName":"1"}),"instanceName":"1"});
            var Q845;
            Q845=makeQuery(id+"F12.opPattern","COPY",BODY,{"derivedFrom":makeQuery(id+"F8.opPattern","COPY",BODY,{"derivedFrom":makeQuery(id+"F7.opPattern","COPY",BODY,{"derivedFrom":makeQuery(id+"F5.opPattern","COPY",BODY,{"derivedFrom":makeQuery(id+"F1.opRevolve","SWEPT_BODY",BODY,{"disambiguationData":[OSD([sQuery(id+"F0.wireOp",EDGE,"E1")])]}),"instanceName":"1"}),"instanceName":"1"}),"instanceName":"1"}),"instanceName":"1"});
            var Q846;
            Q846=makeQuery(id+"F12.opPattern","COPY",BODY,{"derivedFrom":makeQuery(id+"F8.opPattern","COPY",BODY,{"derivedFrom":makeQuery(id+"F7.opPattern","COPY",BODY,{"derivedFrom":makeQuery(id+"F5.opPattern","COPY",BODY,{"derivedFrom":makeQuery(id+"F2.opPattern","COPY",BODY,{"derivedFrom":makeQuery(id+"F1.opRevolve","SWEPT_BODY",BODY,{"disambiguationData":[OSD([sQuery(id+"F0.wireOp",EDGE,"E1")])]}),"instanceName":"1"}),"instanceName":"1"}),"instanceName":"1"}),"instanceName":"1"}),"instanceName":"1"});
            var Q847;
            Q847=makeQuery(id+"F12.opPattern","COPY",BODY,{"derivedFrom":makeQuery(id+"F8.opPattern","COPY",BODY,{"derivedFrom":makeQuery(id+"F7.opPattern","COPY",BODY,{"derivedFrom":makeQuery(id+"F5.opPattern","COPY",BODY,{"derivedFrom":makeQuery(id+"F3.opPattern","COPY",BODY,{"derivedFrom":makeQuery(id+"F2.opPattern","COPY",BODY,{"derivedFrom":makeQuery(id+"F1.opRevolve","SWEPT_BODY",BODY,{"disambiguationData":[OSD([sQuery(id+"F0.wireOp",EDGE,"E1")])]}),"instanceName":"1"}),"instanceName":"1"}),"instanceName":"1"}),"instanceName":"1"}),"instanceName":"1"}),"instanceName":"1"});
            var Q848;
            Q848=makeQuery(id+"F12.opPattern","COPY",BODY,{"derivedFrom":makeQuery(id+"F8.opPattern","COPY",BODY,{"derivedFrom":makeQuery(id+"F7.opPattern","COPY",BODY,{"derivedFrom":makeQuery(id+"F5.opPattern","COPY",BODY,{"derivedFrom":makeQuery(id+"F4.opPattern","COPY",BODY,{"derivedFrom":makeQuery(id+"F1.opRevolve","SWEPT_BODY",BODY,{"disambiguationData":[OSD([sQuery(id+"F0.wireOp",EDGE,"E1")])]}),"instanceName":"1"}),"instanceName":"1"}),"instanceName":"1"}),"instanceName":"1"}),"instanceName":"1"});
            var Q849;
            Q849=makeQuery(id+"F12.opPattern","COPY",BODY,{"derivedFrom":makeQuery(id+"F8.opPattern","COPY",BODY,{"derivedFrom":makeQuery(id+"F7.opPattern","COPY",BODY,{"derivedFrom":makeQuery(id+"F5.opPattern","COPY",BODY,{"derivedFrom":makeQuery(id+"F4.opPattern","COPY",BODY,{"derivedFrom":makeQuery(id+"F2.opPattern","COPY",BODY,{"derivedFrom":makeQuery(id+"F1.opRevolve","SWEPT_BODY",BODY,{"disambiguationData":[OSD([sQuery(id+"F0.wireOp",EDGE,"E1")])]}),"instanceName":"1"}),"instanceName":"1"}),"instanceName":"1"}),"instanceName":"1"}),"instanceName":"1"}),"instanceName":"1"});
            var Q850;
            Q850=makeQuery(id+"F12.opPattern","COPY",BODY,{"derivedFrom":makeQuery(id+"F8.opPattern","COPY",BODY,{"derivedFrom":makeQuery(id+"F7.opPattern","COPY",BODY,{"derivedFrom":makeQuery(id+"F5.opPattern","COPY",BODY,{"derivedFrom":makeQuery(id+"F4.opPattern","COPY",BODY,{"derivedFrom":makeQuery(id+"F3.opPattern","COPY",BODY,{"derivedFrom":makeQuery(id+"F2.opPattern","COPY",BODY,{"derivedFrom":makeQuery(id+"F1.opRevolve","SWEPT_BODY",BODY,{"disambiguationData":[OSD([sQuery(id+"F0.wireOp",EDGE,"E1")])]}),"instanceName":"1"}),"instanceName":"1"}),"instanceName":"1"}),"instanceName":"1"}),"instanceName":"1"}),"instanceName":"1"}),"instanceName":"1"});
            var Q851;
            Q851=makeQuery(id+"F12.opPattern","COPY",BODY,{"derivedFrom":makeQuery(id+"F8.opPattern","COPY",BODY,{"derivedFrom":makeQuery(id+"F7.opPattern","COPY",BODY,{"derivedFrom":makeQuery(id+"F6.opPattern","COPY",BODY,{"derivedFrom":makeQuery(id+"F1.opRevolve","SWEPT_BODY",BODY,{"disambiguationData":[OSD([sQuery(id+"F0.wireOp",EDGE,"E1")])]}),"instanceName":"1"}),"instanceName":"1"}),"instanceName":"1"}),"instanceName":"1"});
            var Q852;
            Q852=makeQuery(id+"F12.opPattern","COPY",BODY,{"derivedFrom":makeQuery(id+"F8.opPattern","COPY",BODY,{"derivedFrom":makeQuery(id+"F7.opPattern","COPY",BODY,{"derivedFrom":makeQuery(id+"F6.opPattern","COPY",BODY,{"derivedFrom":makeQuery(id+"F2.opPattern","COPY",BODY,{"derivedFrom":makeQuery(id+"F1.opRevolve","SWEPT_BODY",BODY,{"disambiguationData":[OSD([sQuery(id+"F0.wireOp",EDGE,"E1")])]}),"instanceName":"1"}),"instanceName":"1"}),"instanceName":"1"}),"instanceName":"1"}),"instanceName":"1"});
            var Q853;
            Q853=makeQuery(id+"F12.opPattern","COPY",BODY,{"derivedFrom":makeQuery(id+"F8.opPattern","COPY",BODY,{"derivedFrom":makeQuery(id+"F7.opPattern","COPY",BODY,{"derivedFrom":makeQuery(id+"F6.opPattern","COPY",BODY,{"derivedFrom":makeQuery(id+"F3.opPattern","COPY",BODY,{"derivedFrom":makeQuery(id+"F2.opPattern","COPY",BODY,{"derivedFrom":makeQuery(id+"F1.opRevolve","SWEPT_BODY",BODY,{"disambiguationData":[OSD([sQuery(id+"F0.wireOp",EDGE,"E1")])]}),"instanceName":"1"}),"instanceName":"1"}),"instanceName":"1"}),"instanceName":"1"}),"instanceName":"1"}),"instanceName":"1"});
            var Q854;
            Q854=makeQuery(id+"F12.opPattern","COPY",BODY,{"derivedFrom":makeQuery(id+"F8.opPattern","COPY",BODY,{"derivedFrom":makeQuery(id+"F7.opPattern","COPY",BODY,{"derivedFrom":makeQuery(id+"F6.opPattern","COPY",BODY,{"derivedFrom":makeQuery(id+"F4.opPattern","COPY",BODY,{"derivedFrom":makeQuery(id+"F1.opRevolve","SWEPT_BODY",BODY,{"disambiguationData":[OSD([sQuery(id+"F0.wireOp",EDGE,"E1")])]}),"instanceName":"1"}),"instanceName":"1"}),"instanceName":"1"}),"instanceName":"1"}),"instanceName":"1"});
            var Q855;
            Q855=makeQuery(id+"F12.opPattern","COPY",BODY,{"derivedFrom":makeQuery(id+"F8.opPattern","COPY",BODY,{"derivedFrom":makeQuery(id+"F7.opPattern","COPY",BODY,{"derivedFrom":makeQuery(id+"F6.opPattern","COPY",BODY,{"derivedFrom":makeQuery(id+"F4.opPattern","COPY",BODY,{"derivedFrom":makeQuery(id+"F2.opPattern","COPY",BODY,{"derivedFrom":makeQuery(id+"F1.opRevolve","SWEPT_BODY",BODY,{"disambiguationData":[OSD([sQuery(id+"F0.wireOp",EDGE,"E1")])]}),"instanceName":"1"}),"instanceName":"1"}),"instanceName":"1"}),"instanceName":"1"}),"instanceName":"1"}),"instanceName":"1"});
            var Q856;
            Q856=makeQuery(id+"F12.opPattern","COPY",BODY,{"derivedFrom":makeQuery(id+"F8.opPattern","COPY",BODY,{"derivedFrom":makeQuery(id+"F7.opPattern","COPY",BODY,{"derivedFrom":makeQuery(id+"F6.opPattern","COPY",BODY,{"derivedFrom":makeQuery(id+"F4.opPattern","COPY",BODY,{"derivedFrom":makeQuery(id+"F3.opPattern","COPY",BODY,{"derivedFrom":makeQuery(id+"F2.opPattern","COPY",BODY,{"derivedFrom":makeQuery(id+"F1.opRevolve","SWEPT_BODY",BODY,{"disambiguationData":[OSD([sQuery(id+"F0.wireOp",EDGE,"E1")])]}),"instanceName":"1"}),"instanceName":"1"}),"instanceName":"1"}),"instanceName":"1"}),"instanceName":"1"}),"instanceName":"1"}),"instanceName":"1"});
            var Q857;
            Q857=makeQuery(id+"F12.opPattern","COPY",BODY,{"derivedFrom":makeQuery(id+"F8.opPattern","COPY",BODY,{"derivedFrom":makeQuery(id+"F7.opPattern","COPY",BODY,{"derivedFrom":makeQuery(id+"F6.opPattern","COPY",BODY,{"derivedFrom":makeQuery(id+"F5.opPattern","COPY",BODY,{"derivedFrom":makeQuery(id+"F1.opRevolve","SWEPT_BODY",BODY,{"disambiguationData":[OSD([sQuery(id+"F0.wireOp",EDGE,"E1")])]}),"instanceName":"1"}),"instanceName":"1"}),"instanceName":"1"}),"instanceName":"1"}),"instanceName":"1"});
            var Q858;
            Q858=makeQuery(id+"F12.opPattern","COPY",BODY,{"derivedFrom":makeQuery(id+"F8.opPattern","COPY",BODY,{"derivedFrom":makeQuery(id+"F7.opPattern","COPY",BODY,{"derivedFrom":makeQuery(id+"F6.opPattern","COPY",BODY,{"derivedFrom":makeQuery(id+"F5.opPattern","COPY",BODY,{"derivedFrom":makeQuery(id+"F2.opPattern","COPY",BODY,{"derivedFrom":makeQuery(id+"F1.opRevolve","SWEPT_BODY",BODY,{"disambiguationData":[OSD([sQuery(id+"F0.wireOp",EDGE,"E1")])]}),"instanceName":"1"}),"instanceName":"1"}),"instanceName":"1"}),"instanceName":"1"}),"instanceName":"1"}),"instanceName":"1"});
            var Q859;
            Q859=makeQuery(id+"F12.opPattern","COPY",BODY,{"derivedFrom":makeQuery(id+"F8.opPattern","COPY",BODY,{"derivedFrom":makeQuery(id+"F7.opPattern","COPY",BODY,{"derivedFrom":makeQuery(id+"F6.opPattern","COPY",BODY,{"derivedFrom":makeQuery(id+"F5.opPattern","COPY",BODY,{"derivedFrom":makeQuery(id+"F3.opPattern","COPY",BODY,{"derivedFrom":makeQuery(id+"F2.opPattern","COPY",BODY,{"derivedFrom":makeQuery(id+"F1.opRevolve","SWEPT_BODY",BODY,{"disambiguationData":[OSD([sQuery(id+"F0.wireOp",EDGE,"E1")])]}),"instanceName":"1"}),"instanceName":"1"}),"instanceName":"1"}),"instanceName":"1"}),"instanceName":"1"}),"instanceName":"1"}),"instanceName":"1"});
            var Q860;
            Q860=makeQuery(id+"F12.opPattern","COPY",BODY,{"derivedFrom":makeQuery(id+"F8.opPattern","COPY",BODY,{"derivedFrom":makeQuery(id+"F7.opPattern","COPY",BODY,{"derivedFrom":makeQuery(id+"F6.opPattern","COPY",BODY,{"derivedFrom":makeQuery(id+"F5.opPattern","COPY",BODY,{"derivedFrom":makeQuery(id+"F4.opPattern","COPY",BODY,{"derivedFrom":makeQuery(id+"F1.opRevolve","SWEPT_BODY",BODY,{"disambiguationData":[OSD([sQuery(id+"F0.wireOp",EDGE,"E1")])]}),"instanceName":"1"}),"instanceName":"1"}),"instanceName":"1"}),"instanceName":"1"}),"instanceName":"1"}),"instanceName":"1"});
            var Q861;
            Q861=makeQuery(id+"F12.opPattern","COPY",BODY,{"derivedFrom":makeQuery(id+"F8.opPattern","COPY",BODY,{"derivedFrom":makeQuery(id+"F7.opPattern","COPY",BODY,{"derivedFrom":makeQuery(id+"F6.opPattern","COPY",BODY,{"derivedFrom":makeQuery(id+"F5.opPattern","COPY",BODY,{"derivedFrom":makeQuery(id+"F4.opPattern","COPY",BODY,{"derivedFrom":makeQuery(id+"F2.opPattern","COPY",BODY,{"derivedFrom":makeQuery(id+"F1.opRevolve","SWEPT_BODY",BODY,{"disambiguationData":[OSD([sQuery(id+"F0.wireOp",EDGE,"E1")])]}),"instanceName":"1"}),"instanceName":"1"}),"instanceName":"1"}),"instanceName":"1"}),"instanceName":"1"}),"instanceName":"1"}),"instanceName":"1"});
            var Q862;
            Q862=makeQuery(id+"F12.opPattern","COPY",BODY,{"derivedFrom":makeQuery(id+"F8.opPattern","COPY",BODY,{"derivedFrom":makeQuery(id+"F7.opPattern","COPY",BODY,{"derivedFrom":makeQuery(id+"F6.opPattern","COPY",BODY,{"derivedFrom":makeQuery(id+"F5.opPattern","COPY",BODY,{"derivedFrom":makeQuery(id+"F4.opPattern","COPY",BODY,{"derivedFrom":makeQuery(id+"F3.opPattern","COPY",BODY,{"derivedFrom":makeQuery(id+"F2.opPattern","COPY",BODY,{"derivedFrom":makeQuery(id+"F1.opRevolve","SWEPT_BODY",BODY,{"disambiguationData":[OSD([sQuery(id+"F0.wireOp",EDGE,"E1")])]}),"instanceName":"1"}),"instanceName":"1"}),"instanceName":"1"}),"instanceName":"1"}),"instanceName":"1"}),"instanceName":"1"}),"instanceName":"1"}),"instanceName":"1"});
            var Q863;
            Q863=makeQuery(id+"F12.opPattern","COPY",BODY,{"derivedFrom":makeQuery(id+"F9.opPattern","COPY",BODY,{"derivedFrom":makeQuery(id+"F1.opRevolve","SWEPT_BODY",BODY,{"disambiguationData":[OSD([sQuery(id+"F0.wireOp",EDGE,"E1")])]}),"instanceName":"1"}),"instanceName":"1"});
            var Q864;
            Q864=makeQuery(id+"F12.opPattern","COPY",BODY,{"derivedFrom":makeQuery(id+"F9.opPattern","COPY",BODY,{"derivedFrom":makeQuery(id+"F2.opPattern","COPY",BODY,{"derivedFrom":makeQuery(id+"F1.opRevolve","SWEPT_BODY",BODY,{"disambiguationData":[OSD([sQuery(id+"F0.wireOp",EDGE,"E1")])]}),"instanceName":"1"}),"instanceName":"1"}),"instanceName":"1"});
            var Q865;
            Q865=makeQuery(id+"F12.opPattern","COPY",BODY,{"derivedFrom":makeQuery(id+"F9.opPattern","COPY",BODY,{"derivedFrom":makeQuery(id+"F3.opPattern","COPY",BODY,{"derivedFrom":makeQuery(id+"F2.opPattern","COPY",BODY,{"derivedFrom":makeQuery(id+"F1.opRevolve","SWEPT_BODY",BODY,{"disambiguationData":[OSD([sQuery(id+"F0.wireOp",EDGE,"E1")])]}),"instanceName":"1"}),"instanceName":"1"}),"instanceName":"1"}),"instanceName":"1"});
            var Q866;
            Q866=makeQuery(id+"F12.opPattern","COPY",BODY,{"derivedFrom":makeQuery(id+"F9.opPattern","COPY",BODY,{"derivedFrom":makeQuery(id+"F4.opPattern","COPY",BODY,{"derivedFrom":makeQuery(id+"F1.opRevolve","SWEPT_BODY",BODY,{"disambiguationData":[OSD([sQuery(id+"F0.wireOp",EDGE,"E1")])]}),"instanceName":"1"}),"instanceName":"1"}),"instanceName":"1"});
            var Q867;
            Q867=makeQuery(id+"F12.opPattern","COPY",BODY,{"derivedFrom":makeQuery(id+"F9.opPattern","COPY",BODY,{"derivedFrom":makeQuery(id+"F4.opPattern","COPY",BODY,{"derivedFrom":makeQuery(id+"F2.opPattern","COPY",BODY,{"derivedFrom":makeQuery(id+"F1.opRevolve","SWEPT_BODY",BODY,{"disambiguationData":[OSD([sQuery(id+"F0.wireOp",EDGE,"E1")])]}),"instanceName":"1"}),"instanceName":"1"}),"instanceName":"1"}),"instanceName":"1"});
            var Q868;
            Q868=makeQuery(id+"F12.opPattern","COPY",BODY,{"derivedFrom":makeQuery(id+"F9.opPattern","COPY",BODY,{"derivedFrom":makeQuery(id+"F4.opPattern","COPY",BODY,{"derivedFrom":makeQuery(id+"F3.opPattern","COPY",BODY,{"derivedFrom":makeQuery(id+"F2.opPattern","COPY",BODY,{"derivedFrom":makeQuery(id+"F1.opRevolve","SWEPT_BODY",BODY,{"disambiguationData":[OSD([sQuery(id+"F0.wireOp",EDGE,"E1")])]}),"instanceName":"1"}),"instanceName":"1"}),"instanceName":"1"}),"instanceName":"1"}),"instanceName":"1"});
            var Q869;
            Q869=makeQuery(id+"F12.opPattern","COPY",BODY,{"derivedFrom":makeQuery(id+"F9.opPattern","COPY",BODY,{"derivedFrom":makeQuery(id+"F5.opPattern","COPY",BODY,{"derivedFrom":makeQuery(id+"F1.opRevolve","SWEPT_BODY",BODY,{"disambiguationData":[OSD([sQuery(id+"F0.wireOp",EDGE,"E1")])]}),"instanceName":"1"}),"instanceName":"1"}),"instanceName":"1"});
            var Q870;
            Q870=makeQuery(id+"F12.opPattern","COPY",BODY,{"derivedFrom":makeQuery(id+"F9.opPattern","COPY",BODY,{"derivedFrom":makeQuery(id+"F5.opPattern","COPY",BODY,{"derivedFrom":makeQuery(id+"F2.opPattern","COPY",BODY,{"derivedFrom":makeQuery(id+"F1.opRevolve","SWEPT_BODY",BODY,{"disambiguationData":[OSD([sQuery(id+"F0.wireOp",EDGE,"E1")])]}),"instanceName":"1"}),"instanceName":"1"}),"instanceName":"1"}),"instanceName":"1"});
            var Q871;
            Q871=makeQuery(id+"F12.opPattern","COPY",BODY,{"derivedFrom":makeQuery(id+"F9.opPattern","COPY",BODY,{"derivedFrom":makeQuery(id+"F5.opPattern","COPY",BODY,{"derivedFrom":makeQuery(id+"F3.opPattern","COPY",BODY,{"derivedFrom":makeQuery(id+"F2.opPattern","COPY",BODY,{"derivedFrom":makeQuery(id+"F1.opRevolve","SWEPT_BODY",BODY,{"disambiguationData":[OSD([sQuery(id+"F0.wireOp",EDGE,"E1")])]}),"instanceName":"1"}),"instanceName":"1"}),"instanceName":"1"}),"instanceName":"1"}),"instanceName":"1"});
            var Q872;
            Q872=makeQuery(id+"F12.opPattern","COPY",BODY,{"derivedFrom":makeQuery(id+"F9.opPattern","COPY",BODY,{"derivedFrom":makeQuery(id+"F5.opPattern","COPY",BODY,{"derivedFrom":makeQuery(id+"F4.opPattern","COPY",BODY,{"derivedFrom":makeQuery(id+"F1.opRevolve","SWEPT_BODY",BODY,{"disambiguationData":[OSD([sQuery(id+"F0.wireOp",EDGE,"E1")])]}),"instanceName":"1"}),"instanceName":"1"}),"instanceName":"1"}),"instanceName":"1"});
            var Q873;
            Q873=makeQuery(id+"F12.opPattern","COPY",BODY,{"derivedFrom":makeQuery(id+"F9.opPattern","COPY",BODY,{"derivedFrom":makeQuery(id+"F5.opPattern","COPY",BODY,{"derivedFrom":makeQuery(id+"F4.opPattern","COPY",BODY,{"derivedFrom":makeQuery(id+"F2.opPattern","COPY",BODY,{"derivedFrom":makeQuery(id+"F1.opRevolve","SWEPT_BODY",BODY,{"disambiguationData":[OSD([sQuery(id+"F0.wireOp",EDGE,"E1")])]}),"instanceName":"1"}),"instanceName":"1"}),"instanceName":"1"}),"instanceName":"1"}),"instanceName":"1"});
            var Q874;
            Q874=makeQuery(id+"F12.opPattern","COPY",BODY,{"derivedFrom":makeQuery(id+"F9.opPattern","COPY",BODY,{"derivedFrom":makeQuery(id+"F5.opPattern","COPY",BODY,{"derivedFrom":makeQuery(id+"F4.opPattern","COPY",BODY,{"derivedFrom":makeQuery(id+"F3.opPattern","COPY",BODY,{"derivedFrom":makeQuery(id+"F2.opPattern","COPY",BODY,{"derivedFrom":makeQuery(id+"F1.opRevolve","SWEPT_BODY",BODY,{"disambiguationData":[OSD([sQuery(id+"F0.wireOp",EDGE,"E1")])]}),"instanceName":"1"}),"instanceName":"1"}),"instanceName":"1"}),"instanceName":"1"}),"instanceName":"1"}),"instanceName":"1"});
            var Q875;
            Q875=makeQuery(id+"F12.opPattern","COPY",BODY,{"derivedFrom":makeQuery(id+"F9.opPattern","COPY",BODY,{"derivedFrom":makeQuery(id+"F6.opPattern","COPY",BODY,{"derivedFrom":makeQuery(id+"F1.opRevolve","SWEPT_BODY",BODY,{"disambiguationData":[OSD([sQuery(id+"F0.wireOp",EDGE,"E1")])]}),"instanceName":"1"}),"instanceName":"1"}),"instanceName":"1"});
            var Q876;
            Q876=makeQuery(id+"F12.opPattern","COPY",BODY,{"derivedFrom":makeQuery(id+"F9.opPattern","COPY",BODY,{"derivedFrom":makeQuery(id+"F6.opPattern","COPY",BODY,{"derivedFrom":makeQuery(id+"F2.opPattern","COPY",BODY,{"derivedFrom":makeQuery(id+"F1.opRevolve","SWEPT_BODY",BODY,{"disambiguationData":[OSD([sQuery(id+"F0.wireOp",EDGE,"E1")])]}),"instanceName":"1"}),"instanceName":"1"}),"instanceName":"1"}),"instanceName":"1"});
            var Q877;
            Q877=makeQuery(id+"F12.opPattern","COPY",BODY,{"derivedFrom":makeQuery(id+"F9.opPattern","COPY",BODY,{"derivedFrom":makeQuery(id+"F6.opPattern","COPY",BODY,{"derivedFrom":makeQuery(id+"F3.opPattern","COPY",BODY,{"derivedFrom":makeQuery(id+"F2.opPattern","COPY",BODY,{"derivedFrom":makeQuery(id+"F1.opRevolve","SWEPT_BODY",BODY,{"disambiguationData":[OSD([sQuery(id+"F0.wireOp",EDGE,"E1")])]}),"instanceName":"1"}),"instanceName":"1"}),"instanceName":"1"}),"instanceName":"1"}),"instanceName":"1"});
            var Q878;
            Q878=makeQuery(id+"F12.opPattern","COPY",BODY,{"derivedFrom":makeQuery(id+"F9.opPattern","COPY",BODY,{"derivedFrom":makeQuery(id+"F6.opPattern","COPY",BODY,{"derivedFrom":makeQuery(id+"F4.opPattern","COPY",BODY,{"derivedFrom":makeQuery(id+"F1.opRevolve","SWEPT_BODY",BODY,{"disambiguationData":[OSD([sQuery(id+"F0.wireOp",EDGE,"E1")])]}),"instanceName":"1"}),"instanceName":"1"}),"instanceName":"1"}),"instanceName":"1"});
            var Q879;
            Q879=makeQuery(id+"F12.opPattern","COPY",BODY,{"derivedFrom":makeQuery(id+"F9.opPattern","COPY",BODY,{"derivedFrom":makeQuery(id+"F6.opPattern","COPY",BODY,{"derivedFrom":makeQuery(id+"F4.opPattern","COPY",BODY,{"derivedFrom":makeQuery(id+"F2.opPattern","COPY",BODY,{"derivedFrom":makeQuery(id+"F1.opRevolve","SWEPT_BODY",BODY,{"disambiguationData":[OSD([sQuery(id+"F0.wireOp",EDGE,"E1")])]}),"instanceName":"1"}),"instanceName":"1"}),"instanceName":"1"}),"instanceName":"1"}),"instanceName":"1"});
            var Q880;
            Q880=makeQuery(id+"F12.opPattern","COPY",BODY,{"derivedFrom":makeQuery(id+"F9.opPattern","COPY",BODY,{"derivedFrom":makeQuery(id+"F6.opPattern","COPY",BODY,{"derivedFrom":makeQuery(id+"F4.opPattern","COPY",BODY,{"derivedFrom":makeQuery(id+"F3.opPattern","COPY",BODY,{"derivedFrom":makeQuery(id+"F2.opPattern","COPY",BODY,{"derivedFrom":makeQuery(id+"F1.opRevolve","SWEPT_BODY",BODY,{"disambiguationData":[OSD([sQuery(id+"F0.wireOp",EDGE,"E1")])]}),"instanceName":"1"}),"instanceName":"1"}),"instanceName":"1"}),"instanceName":"1"}),"instanceName":"1"}),"instanceName":"1"});
            var Q881;
            Q881=makeQuery(id+"F12.opPattern","COPY",BODY,{"derivedFrom":makeQuery(id+"F9.opPattern","COPY",BODY,{"derivedFrom":makeQuery(id+"F6.opPattern","COPY",BODY,{"derivedFrom":makeQuery(id+"F5.opPattern","COPY",BODY,{"derivedFrom":makeQuery(id+"F1.opRevolve","SWEPT_BODY",BODY,{"disambiguationData":[OSD([sQuery(id+"F0.wireOp",EDGE,"E1")])]}),"instanceName":"1"}),"instanceName":"1"}),"instanceName":"1"}),"instanceName":"1"});
            var Q882;
            Q882=makeQuery(id+"F12.opPattern","COPY",BODY,{"derivedFrom":makeQuery(id+"F9.opPattern","COPY",BODY,{"derivedFrom":makeQuery(id+"F6.opPattern","COPY",BODY,{"derivedFrom":makeQuery(id+"F5.opPattern","COPY",BODY,{"derivedFrom":makeQuery(id+"F2.opPattern","COPY",BODY,{"derivedFrom":makeQuery(id+"F1.opRevolve","SWEPT_BODY",BODY,{"disambiguationData":[OSD([sQuery(id+"F0.wireOp",EDGE,"E1")])]}),"instanceName":"1"}),"instanceName":"1"}),"instanceName":"1"}),"instanceName":"1"}),"instanceName":"1"});
            var Q883;
            Q883=makeQuery(id+"F12.opPattern","COPY",BODY,{"derivedFrom":makeQuery(id+"F9.opPattern","COPY",BODY,{"derivedFrom":makeQuery(id+"F6.opPattern","COPY",BODY,{"derivedFrom":makeQuery(id+"F5.opPattern","COPY",BODY,{"derivedFrom":makeQuery(id+"F3.opPattern","COPY",BODY,{"derivedFrom":makeQuery(id+"F2.opPattern","COPY",BODY,{"derivedFrom":makeQuery(id+"F1.opRevolve","SWEPT_BODY",BODY,{"disambiguationData":[OSD([sQuery(id+"F0.wireOp",EDGE,"E1")])]}),"instanceName":"1"}),"instanceName":"1"}),"instanceName":"1"}),"instanceName":"1"}),"instanceName":"1"}),"instanceName":"1"});
            var Q884;
            Q884=makeQuery(id+"F12.opPattern","COPY",BODY,{"derivedFrom":makeQuery(id+"F9.opPattern","COPY",BODY,{"derivedFrom":makeQuery(id+"F6.opPattern","COPY",BODY,{"derivedFrom":makeQuery(id+"F5.opPattern","COPY",BODY,{"derivedFrom":makeQuery(id+"F4.opPattern","COPY",BODY,{"derivedFrom":makeQuery(id+"F1.opRevolve","SWEPT_BODY",BODY,{"disambiguationData":[OSD([sQuery(id+"F0.wireOp",EDGE,"E1")])]}),"instanceName":"1"}),"instanceName":"1"}),"instanceName":"1"}),"instanceName":"1"}),"instanceName":"1"});
            var Q885;
            Q885=makeQuery(id+"F12.opPattern","COPY",BODY,{"derivedFrom":makeQuery(id+"F9.opPattern","COPY",BODY,{"derivedFrom":makeQuery(id+"F6.opPattern","COPY",BODY,{"derivedFrom":makeQuery(id+"F5.opPattern","COPY",BODY,{"derivedFrom":makeQuery(id+"F4.opPattern","COPY",BODY,{"derivedFrom":makeQuery(id+"F2.opPattern","COPY",BODY,{"derivedFrom":makeQuery(id+"F1.opRevolve","SWEPT_BODY",BODY,{"disambiguationData":[OSD([sQuery(id+"F0.wireOp",EDGE,"E1")])]}),"instanceName":"1"}),"instanceName":"1"}),"instanceName":"1"}),"instanceName":"1"}),"instanceName":"1"}),"instanceName":"1"});
            var Q886;
            Q886=makeQuery(id+"F12.opPattern","COPY",BODY,{"derivedFrom":makeQuery(id+"F9.opPattern","COPY",BODY,{"derivedFrom":makeQuery(id+"F6.opPattern","COPY",BODY,{"derivedFrom":makeQuery(id+"F5.opPattern","COPY",BODY,{"derivedFrom":makeQuery(id+"F4.opPattern","COPY",BODY,{"derivedFrom":makeQuery(id+"F3.opPattern","COPY",BODY,{"derivedFrom":makeQuery(id+"F2.opPattern","COPY",BODY,{"derivedFrom":makeQuery(id+"F1.opRevolve","SWEPT_BODY",BODY,{"disambiguationData":[OSD([sQuery(id+"F0.wireOp",EDGE,"E1")])]}),"instanceName":"1"}),"instanceName":"1"}),"instanceName":"1"}),"instanceName":"1"}),"instanceName":"1"}),"instanceName":"1"}),"instanceName":"1"});
            var Q887;
            Q887=makeQuery(id+"F12.opPattern","COPY",BODY,{"derivedFrom":makeQuery(id+"F9.opPattern","COPY",BODY,{"derivedFrom":makeQuery(id+"F7.opPattern","COPY",BODY,{"derivedFrom":makeQuery(id+"F1.opRevolve","SWEPT_BODY",BODY,{"disambiguationData":[OSD([sQuery(id+"F0.wireOp",EDGE,"E1")])]}),"instanceName":"1"}),"instanceName":"1"}),"instanceName":"1"});
            var Q888;
            Q888=makeQuery(id+"F12.opPattern","COPY",BODY,{"derivedFrom":makeQuery(id+"F9.opPattern","COPY",BODY,{"derivedFrom":makeQuery(id+"F7.opPattern","COPY",BODY,{"derivedFrom":makeQuery(id+"F2.opPattern","COPY",BODY,{"derivedFrom":makeQuery(id+"F1.opRevolve","SWEPT_BODY",BODY,{"disambiguationData":[OSD([sQuery(id+"F0.wireOp",EDGE,"E1")])]}),"instanceName":"1"}),"instanceName":"1"}),"instanceName":"1"}),"instanceName":"1"});
            var Q889;
            Q889=makeQuery(id+"F12.opPattern","COPY",BODY,{"derivedFrom":makeQuery(id+"F9.opPattern","COPY",BODY,{"derivedFrom":makeQuery(id+"F7.opPattern","COPY",BODY,{"derivedFrom":makeQuery(id+"F3.opPattern","COPY",BODY,{"derivedFrom":makeQuery(id+"F2.opPattern","COPY",BODY,{"derivedFrom":makeQuery(id+"F1.opRevolve","SWEPT_BODY",BODY,{"disambiguationData":[OSD([sQuery(id+"F0.wireOp",EDGE,"E1")])]}),"instanceName":"1"}),"instanceName":"1"}),"instanceName":"1"}),"instanceName":"1"}),"instanceName":"1"});
            var Q890;
            Q890=makeQuery(id+"F12.opPattern","COPY",BODY,{"derivedFrom":makeQuery(id+"F9.opPattern","COPY",BODY,{"derivedFrom":makeQuery(id+"F7.opPattern","COPY",BODY,{"derivedFrom":makeQuery(id+"F4.opPattern","COPY",BODY,{"derivedFrom":makeQuery(id+"F1.opRevolve","SWEPT_BODY",BODY,{"disambiguationData":[OSD([sQuery(id+"F0.wireOp",EDGE,"E1")])]}),"instanceName":"1"}),"instanceName":"1"}),"instanceName":"1"}),"instanceName":"1"});
            var Q891;
            Q891=makeQuery(id+"F12.opPattern","COPY",BODY,{"derivedFrom":makeQuery(id+"F9.opPattern","COPY",BODY,{"derivedFrom":makeQuery(id+"F7.opPattern","COPY",BODY,{"derivedFrom":makeQuery(id+"F4.opPattern","COPY",BODY,{"derivedFrom":makeQuery(id+"F2.opPattern","COPY",BODY,{"derivedFrom":makeQuery(id+"F1.opRevolve","SWEPT_BODY",BODY,{"disambiguationData":[OSD([sQuery(id+"F0.wireOp",EDGE,"E1")])]}),"instanceName":"1"}),"instanceName":"1"}),"instanceName":"1"}),"instanceName":"1"}),"instanceName":"1"});
            var Q892;
            Q892=makeQuery(id+"F12.opPattern","COPY",BODY,{"derivedFrom":makeQuery(id+"F9.opPattern","COPY",BODY,{"derivedFrom":makeQuery(id+"F7.opPattern","COPY",BODY,{"derivedFrom":makeQuery(id+"F4.opPattern","COPY",BODY,{"derivedFrom":makeQuery(id+"F3.opPattern","COPY",BODY,{"derivedFrom":makeQuery(id+"F2.opPattern","COPY",BODY,{"derivedFrom":makeQuery(id+"F1.opRevolve","SWEPT_BODY",BODY,{"disambiguationData":[OSD([sQuery(id+"F0.wireOp",EDGE,"E1")])]}),"instanceName":"1"}),"instanceName":"1"}),"instanceName":"1"}),"instanceName":"1"}),"instanceName":"1"}),"instanceName":"1"});
            var Q893;
            Q893=makeQuery(id+"F12.opPattern","COPY",BODY,{"derivedFrom":makeQuery(id+"F9.opPattern","COPY",BODY,{"derivedFrom":makeQuery(id+"F7.opPattern","COPY",BODY,{"derivedFrom":makeQuery(id+"F5.opPattern","COPY",BODY,{"derivedFrom":makeQuery(id+"F1.opRevolve","SWEPT_BODY",BODY,{"disambiguationData":[OSD([sQuery(id+"F0.wireOp",EDGE,"E1")])]}),"instanceName":"1"}),"instanceName":"1"}),"instanceName":"1"}),"instanceName":"1"});
            var Q894;
            Q894=makeQuery(id+"F12.opPattern","COPY",BODY,{"derivedFrom":makeQuery(id+"F9.opPattern","COPY",BODY,{"derivedFrom":makeQuery(id+"F7.opPattern","COPY",BODY,{"derivedFrom":makeQuery(id+"F5.opPattern","COPY",BODY,{"derivedFrom":makeQuery(id+"F2.opPattern","COPY",BODY,{"derivedFrom":makeQuery(id+"F1.opRevolve","SWEPT_BODY",BODY,{"disambiguationData":[OSD([sQuery(id+"F0.wireOp",EDGE,"E1")])]}),"instanceName":"1"}),"instanceName":"1"}),"instanceName":"1"}),"instanceName":"1"}),"instanceName":"1"});
            var Q895;
            Q895=makeQuery(id+"F12.opPattern","COPY",BODY,{"derivedFrom":makeQuery(id+"F9.opPattern","COPY",BODY,{"derivedFrom":makeQuery(id+"F7.opPattern","COPY",BODY,{"derivedFrom":makeQuery(id+"F5.opPattern","COPY",BODY,{"derivedFrom":makeQuery(id+"F3.opPattern","COPY",BODY,{"derivedFrom":makeQuery(id+"F2.opPattern","COPY",BODY,{"derivedFrom":makeQuery(id+"F1.opRevolve","SWEPT_BODY",BODY,{"disambiguationData":[OSD([sQuery(id+"F0.wireOp",EDGE,"E1")])]}),"instanceName":"1"}),"instanceName":"1"}),"instanceName":"1"}),"instanceName":"1"}),"instanceName":"1"}),"instanceName":"1"});
            var Q896;
            Q896=makeQuery(id+"F12.opPattern","COPY",BODY,{"derivedFrom":makeQuery(id+"F9.opPattern","COPY",BODY,{"derivedFrom":makeQuery(id+"F7.opPattern","COPY",BODY,{"derivedFrom":makeQuery(id+"F5.opPattern","COPY",BODY,{"derivedFrom":makeQuery(id+"F4.opPattern","COPY",BODY,{"derivedFrom":makeQuery(id+"F1.opRevolve","SWEPT_BODY",BODY,{"disambiguationData":[OSD([sQuery(id+"F0.wireOp",EDGE,"E1")])]}),"instanceName":"1"}),"instanceName":"1"}),"instanceName":"1"}),"instanceName":"1"}),"instanceName":"1"});
            var Q897;
            Q897=makeQuery(id+"F12.opPattern","COPY",BODY,{"derivedFrom":makeQuery(id+"F9.opPattern","COPY",BODY,{"derivedFrom":makeQuery(id+"F7.opPattern","COPY",BODY,{"derivedFrom":makeQuery(id+"F5.opPattern","COPY",BODY,{"derivedFrom":makeQuery(id+"F4.opPattern","COPY",BODY,{"derivedFrom":makeQuery(id+"F2.opPattern","COPY",BODY,{"derivedFrom":makeQuery(id+"F1.opRevolve","SWEPT_BODY",BODY,{"disambiguationData":[OSD([sQuery(id+"F0.wireOp",EDGE,"E1")])]}),"instanceName":"1"}),"instanceName":"1"}),"instanceName":"1"}),"instanceName":"1"}),"instanceName":"1"}),"instanceName":"1"});
            var Q898;
            Q898=makeQuery(id+"F12.opPattern","COPY",BODY,{"derivedFrom":makeQuery(id+"F9.opPattern","COPY",BODY,{"derivedFrom":makeQuery(id+"F7.opPattern","COPY",BODY,{"derivedFrom":makeQuery(id+"F5.opPattern","COPY",BODY,{"derivedFrom":makeQuery(id+"F4.opPattern","COPY",BODY,{"derivedFrom":makeQuery(id+"F3.opPattern","COPY",BODY,{"derivedFrom":makeQuery(id+"F2.opPattern","COPY",BODY,{"derivedFrom":makeQuery(id+"F1.opRevolve","SWEPT_BODY",BODY,{"disambiguationData":[OSD([sQuery(id+"F0.wireOp",EDGE,"E1")])]}),"instanceName":"1"}),"instanceName":"1"}),"instanceName":"1"}),"instanceName":"1"}),"instanceName":"1"}),"instanceName":"1"}),"instanceName":"1"});
            var Q899;
            Q899=makeQuery(id+"F12.opPattern","COPY",BODY,{"derivedFrom":makeQuery(id+"F9.opPattern","COPY",BODY,{"derivedFrom":makeQuery(id+"F7.opPattern","COPY",BODY,{"derivedFrom":makeQuery(id+"F6.opPattern","COPY",BODY,{"derivedFrom":makeQuery(id+"F1.opRevolve","SWEPT_BODY",BODY,{"disambiguationData":[OSD([sQuery(id+"F0.wireOp",EDGE,"E1")])]}),"instanceName":"1"}),"instanceName":"1"}),"instanceName":"1"}),"instanceName":"1"});
            var Q900;
            Q900=makeQuery(id+"F12.opPattern","COPY",BODY,{"derivedFrom":makeQuery(id+"F9.opPattern","COPY",BODY,{"derivedFrom":makeQuery(id+"F7.opPattern","COPY",BODY,{"derivedFrom":makeQuery(id+"F6.opPattern","COPY",BODY,{"derivedFrom":makeQuery(id+"F2.opPattern","COPY",BODY,{"derivedFrom":makeQuery(id+"F1.opRevolve","SWEPT_BODY",BODY,{"disambiguationData":[OSD([sQuery(id+"F0.wireOp",EDGE,"E1")])]}),"instanceName":"1"}),"instanceName":"1"}),"instanceName":"1"}),"instanceName":"1"}),"instanceName":"1"});
            var Q901;
            Q901=makeQuery(id+"F12.opPattern","COPY",BODY,{"derivedFrom":makeQuery(id+"F9.opPattern","COPY",BODY,{"derivedFrom":makeQuery(id+"F7.opPattern","COPY",BODY,{"derivedFrom":makeQuery(id+"F6.opPattern","COPY",BODY,{"derivedFrom":makeQuery(id+"F3.opPattern","COPY",BODY,{"derivedFrom":makeQuery(id+"F2.opPattern","COPY",BODY,{"derivedFrom":makeQuery(id+"F1.opRevolve","SWEPT_BODY",BODY,{"disambiguationData":[OSD([sQuery(id+"F0.wireOp",EDGE,"E1")])]}),"instanceName":"1"}),"instanceName":"1"}),"instanceName":"1"}),"instanceName":"1"}),"instanceName":"1"}),"instanceName":"1"});
            var Q902;
            Q902=makeQuery(id+"F12.opPattern","COPY",BODY,{"derivedFrom":makeQuery(id+"F9.opPattern","COPY",BODY,{"derivedFrom":makeQuery(id+"F7.opPattern","COPY",BODY,{"derivedFrom":makeQuery(id+"F6.opPattern","COPY",BODY,{"derivedFrom":makeQuery(id+"F4.opPattern","COPY",BODY,{"derivedFrom":makeQuery(id+"F1.opRevolve","SWEPT_BODY",BODY,{"disambiguationData":[OSD([sQuery(id+"F0.wireOp",EDGE,"E1")])]}),"instanceName":"1"}),"instanceName":"1"}),"instanceName":"1"}),"instanceName":"1"}),"instanceName":"1"});
            var Q903;
            Q903=makeQuery(id+"F12.opPattern","COPY",BODY,{"derivedFrom":makeQuery(id+"F9.opPattern","COPY",BODY,{"derivedFrom":makeQuery(id+"F7.opPattern","COPY",BODY,{"derivedFrom":makeQuery(id+"F6.opPattern","COPY",BODY,{"derivedFrom":makeQuery(id+"F4.opPattern","COPY",BODY,{"derivedFrom":makeQuery(id+"F2.opPattern","COPY",BODY,{"derivedFrom":makeQuery(id+"F1.opRevolve","SWEPT_BODY",BODY,{"disambiguationData":[OSD([sQuery(id+"F0.wireOp",EDGE,"E1")])]}),"instanceName":"1"}),"instanceName":"1"}),"instanceName":"1"}),"instanceName":"1"}),"instanceName":"1"}),"instanceName":"1"});
            var Q904;
            Q904=makeQuery(id+"F12.opPattern","COPY",BODY,{"derivedFrom":makeQuery(id+"F9.opPattern","COPY",BODY,{"derivedFrom":makeQuery(id+"F7.opPattern","COPY",BODY,{"derivedFrom":makeQuery(id+"F6.opPattern","COPY",BODY,{"derivedFrom":makeQuery(id+"F4.opPattern","COPY",BODY,{"derivedFrom":makeQuery(id+"F3.opPattern","COPY",BODY,{"derivedFrom":makeQuery(id+"F2.opPattern","COPY",BODY,{"derivedFrom":makeQuery(id+"F1.opRevolve","SWEPT_BODY",BODY,{"disambiguationData":[OSD([sQuery(id+"F0.wireOp",EDGE,"E1")])]}),"instanceName":"1"}),"instanceName":"1"}),"instanceName":"1"}),"instanceName":"1"}),"instanceName":"1"}),"instanceName":"1"}),"instanceName":"1"});
            var Q905;
            Q905=makeQuery(id+"F12.opPattern","COPY",BODY,{"derivedFrom":makeQuery(id+"F9.opPattern","COPY",BODY,{"derivedFrom":makeQuery(id+"F7.opPattern","COPY",BODY,{"derivedFrom":makeQuery(id+"F6.opPattern","COPY",BODY,{"derivedFrom":makeQuery(id+"F5.opPattern","COPY",BODY,{"derivedFrom":makeQuery(id+"F1.opRevolve","SWEPT_BODY",BODY,{"disambiguationData":[OSD([sQuery(id+"F0.wireOp",EDGE,"E1")])]}),"instanceName":"1"}),"instanceName":"1"}),"instanceName":"1"}),"instanceName":"1"}),"instanceName":"1"});
            var Q906;
            Q906=makeQuery(id+"F12.opPattern","COPY",BODY,{"derivedFrom":makeQuery(id+"F9.opPattern","COPY",BODY,{"derivedFrom":makeQuery(id+"F7.opPattern","COPY",BODY,{"derivedFrom":makeQuery(id+"F6.opPattern","COPY",BODY,{"derivedFrom":makeQuery(id+"F5.opPattern","COPY",BODY,{"derivedFrom":makeQuery(id+"F2.opPattern","COPY",BODY,{"derivedFrom":makeQuery(id+"F1.opRevolve","SWEPT_BODY",BODY,{"disambiguationData":[OSD([sQuery(id+"F0.wireOp",EDGE,"E1")])]}),"instanceName":"1"}),"instanceName":"1"}),"instanceName":"1"}),"instanceName":"1"}),"instanceName":"1"}),"instanceName":"1"});
            var Q907;
            Q907=makeQuery(id+"F12.opPattern","COPY",BODY,{"derivedFrom":makeQuery(id+"F9.opPattern","COPY",BODY,{"derivedFrom":makeQuery(id+"F7.opPattern","COPY",BODY,{"derivedFrom":makeQuery(id+"F6.opPattern","COPY",BODY,{"derivedFrom":makeQuery(id+"F5.opPattern","COPY",BODY,{"derivedFrom":makeQuery(id+"F3.opPattern","COPY",BODY,{"derivedFrom":makeQuery(id+"F2.opPattern","COPY",BODY,{"derivedFrom":makeQuery(id+"F1.opRevolve","SWEPT_BODY",BODY,{"disambiguationData":[OSD([sQuery(id+"F0.wireOp",EDGE,"E1")])]}),"instanceName":"1"}),"instanceName":"1"}),"instanceName":"1"}),"instanceName":"1"}),"instanceName":"1"}),"instanceName":"1"}),"instanceName":"1"});
            var Q908;
            Q908=makeQuery(id+"F12.opPattern","COPY",BODY,{"derivedFrom":makeQuery(id+"F9.opPattern","COPY",BODY,{"derivedFrom":makeQuery(id+"F7.opPattern","COPY",BODY,{"derivedFrom":makeQuery(id+"F6.opPattern","COPY",BODY,{"derivedFrom":makeQuery(id+"F5.opPattern","COPY",BODY,{"derivedFrom":makeQuery(id+"F4.opPattern","COPY",BODY,{"derivedFrom":makeQuery(id+"F1.opRevolve","SWEPT_BODY",BODY,{"disambiguationData":[OSD([sQuery(id+"F0.wireOp",EDGE,"E1")])]}),"instanceName":"1"}),"instanceName":"1"}),"instanceName":"1"}),"instanceName":"1"}),"instanceName":"1"}),"instanceName":"1"});
            var Q909;
            Q909=makeQuery(id+"F12.opPattern","COPY",BODY,{"derivedFrom":makeQuery(id+"F9.opPattern","COPY",BODY,{"derivedFrom":makeQuery(id+"F7.opPattern","COPY",BODY,{"derivedFrom":makeQuery(id+"F6.opPattern","COPY",BODY,{"derivedFrom":makeQuery(id+"F5.opPattern","COPY",BODY,{"derivedFrom":makeQuery(id+"F4.opPattern","COPY",BODY,{"derivedFrom":makeQuery(id+"F2.opPattern","COPY",BODY,{"derivedFrom":makeQuery(id+"F1.opRevolve","SWEPT_BODY",BODY,{"disambiguationData":[OSD([sQuery(id+"F0.wireOp",EDGE,"E1")])]}),"instanceName":"1"}),"instanceName":"1"}),"instanceName":"1"}),"instanceName":"1"}),"instanceName":"1"}),"instanceName":"1"}),"instanceName":"1"});
            var Q910;
            Q910=makeQuery(id+"F12.opPattern","COPY",BODY,{"derivedFrom":makeQuery(id+"F9.opPattern","COPY",BODY,{"derivedFrom":makeQuery(id+"F7.opPattern","COPY",BODY,{"derivedFrom":makeQuery(id+"F6.opPattern","COPY",BODY,{"derivedFrom":makeQuery(id+"F5.opPattern","COPY",BODY,{"derivedFrom":makeQuery(id+"F4.opPattern","COPY",BODY,{"derivedFrom":makeQuery(id+"F3.opPattern","COPY",BODY,{"derivedFrom":makeQuery(id+"F2.opPattern","COPY",BODY,{"derivedFrom":makeQuery(id+"F1.opRevolve","SWEPT_BODY",BODY,{"disambiguationData":[OSD([sQuery(id+"F0.wireOp",EDGE,"E1")])]}),"instanceName":"1"}),"instanceName":"1"}),"instanceName":"1"}),"instanceName":"1"}),"instanceName":"1"}),"instanceName":"1"}),"instanceName":"1"}),"instanceName":"1"});
            var Q911;
            Q911=makeQuery(id+"F12.opPattern","COPY",BODY,{"derivedFrom":makeQuery(id+"F9.opPattern","COPY",BODY,{"derivedFrom":makeQuery(id+"F8.opPattern","COPY",BODY,{"derivedFrom":makeQuery(id+"F1.opRevolve","SWEPT_BODY",BODY,{"disambiguationData":[OSD([sQuery(id+"F0.wireOp",EDGE,"E1")])]}),"instanceName":"1"}),"instanceName":"1"}),"instanceName":"1"});
            var Q912;
            Q912=makeQuery(id+"F12.opPattern","COPY",BODY,{"derivedFrom":makeQuery(id+"F9.opPattern","COPY",BODY,{"derivedFrom":makeQuery(id+"F8.opPattern","COPY",BODY,{"derivedFrom":makeQuery(id+"F2.opPattern","COPY",BODY,{"derivedFrom":makeQuery(id+"F1.opRevolve","SWEPT_BODY",BODY,{"disambiguationData":[OSD([sQuery(id+"F0.wireOp",EDGE,"E1")])]}),"instanceName":"1"}),"instanceName":"1"}),"instanceName":"1"}),"instanceName":"1"});
            var Q913;
            Q913=makeQuery(id+"F12.opPattern","COPY",BODY,{"derivedFrom":makeQuery(id+"F9.opPattern","COPY",BODY,{"derivedFrom":makeQuery(id+"F8.opPattern","COPY",BODY,{"derivedFrom":makeQuery(id+"F3.opPattern","COPY",BODY,{"derivedFrom":makeQuery(id+"F2.opPattern","COPY",BODY,{"derivedFrom":makeQuery(id+"F1.opRevolve","SWEPT_BODY",BODY,{"disambiguationData":[OSD([sQuery(id+"F0.wireOp",EDGE,"E1")])]}),"instanceName":"1"}),"instanceName":"1"}),"instanceName":"1"}),"instanceName":"1"}),"instanceName":"1"});
            var Q914;
            Q914=makeQuery(id+"F12.opPattern","COPY",BODY,{"derivedFrom":makeQuery(id+"F9.opPattern","COPY",BODY,{"derivedFrom":makeQuery(id+"F8.opPattern","COPY",BODY,{"derivedFrom":makeQuery(id+"F4.opPattern","COPY",BODY,{"derivedFrom":makeQuery(id+"F1.opRevolve","SWEPT_BODY",BODY,{"disambiguationData":[OSD([sQuery(id+"F0.wireOp",EDGE,"E1")])]}),"instanceName":"1"}),"instanceName":"1"}),"instanceName":"1"}),"instanceName":"1"});
            var Q915;
            Q915=makeQuery(id+"F12.opPattern","COPY",BODY,{"derivedFrom":makeQuery(id+"F9.opPattern","COPY",BODY,{"derivedFrom":makeQuery(id+"F8.opPattern","COPY",BODY,{"derivedFrom":makeQuery(id+"F4.opPattern","COPY",BODY,{"derivedFrom":makeQuery(id+"F2.opPattern","COPY",BODY,{"derivedFrom":makeQuery(id+"F1.opRevolve","SWEPT_BODY",BODY,{"disambiguationData":[OSD([sQuery(id+"F0.wireOp",EDGE,"E1")])]}),"instanceName":"1"}),"instanceName":"1"}),"instanceName":"1"}),"instanceName":"1"}),"instanceName":"1"});
            var Q916;
            Q916=makeQuery(id+"F12.opPattern","COPY",BODY,{"derivedFrom":makeQuery(id+"F9.opPattern","COPY",BODY,{"derivedFrom":makeQuery(id+"F8.opPattern","COPY",BODY,{"derivedFrom":makeQuery(id+"F4.opPattern","COPY",BODY,{"derivedFrom":makeQuery(id+"F3.opPattern","COPY",BODY,{"derivedFrom":makeQuery(id+"F2.opPattern","COPY",BODY,{"derivedFrom":makeQuery(id+"F1.opRevolve","SWEPT_BODY",BODY,{"disambiguationData":[OSD([sQuery(id+"F0.wireOp",EDGE,"E1")])]}),"instanceName":"1"}),"instanceName":"1"}),"instanceName":"1"}),"instanceName":"1"}),"instanceName":"1"}),"instanceName":"1"});
            var Q917;
            Q917=makeQuery(id+"F12.opPattern","COPY",BODY,{"derivedFrom":makeQuery(id+"F9.opPattern","COPY",BODY,{"derivedFrom":makeQuery(id+"F8.opPattern","COPY",BODY,{"derivedFrom":makeQuery(id+"F5.opPattern","COPY",BODY,{"derivedFrom":makeQuery(id+"F1.opRevolve","SWEPT_BODY",BODY,{"disambiguationData":[OSD([sQuery(id+"F0.wireOp",EDGE,"E1")])]}),"instanceName":"1"}),"instanceName":"1"}),"instanceName":"1"}),"instanceName":"1"});
            var Q918;
            Q918=makeQuery(id+"F12.opPattern","COPY",BODY,{"derivedFrom":makeQuery(id+"F9.opPattern","COPY",BODY,{"derivedFrom":makeQuery(id+"F8.opPattern","COPY",BODY,{"derivedFrom":makeQuery(id+"F5.opPattern","COPY",BODY,{"derivedFrom":makeQuery(id+"F2.opPattern","COPY",BODY,{"derivedFrom":makeQuery(id+"F1.opRevolve","SWEPT_BODY",BODY,{"disambiguationData":[OSD([sQuery(id+"F0.wireOp",EDGE,"E1")])]}),"instanceName":"1"}),"instanceName":"1"}),"instanceName":"1"}),"instanceName":"1"}),"instanceName":"1"});
            var Q919;
            Q919=makeQuery(id+"F12.opPattern","COPY",BODY,{"derivedFrom":makeQuery(id+"F9.opPattern","COPY",BODY,{"derivedFrom":makeQuery(id+"F8.opPattern","COPY",BODY,{"derivedFrom":makeQuery(id+"F5.opPattern","COPY",BODY,{"derivedFrom":makeQuery(id+"F3.opPattern","COPY",BODY,{"derivedFrom":makeQuery(id+"F2.opPattern","COPY",BODY,{"derivedFrom":makeQuery(id+"F1.opRevolve","SWEPT_BODY",BODY,{"disambiguationData":[OSD([sQuery(id+"F0.wireOp",EDGE,"E1")])]}),"instanceName":"1"}),"instanceName":"1"}),"instanceName":"1"}),"instanceName":"1"}),"instanceName":"1"}),"instanceName":"1"});
            var Q920;
            Q920=makeQuery(id+"F12.opPattern","COPY",BODY,{"derivedFrom":makeQuery(id+"F9.opPattern","COPY",BODY,{"derivedFrom":makeQuery(id+"F8.opPattern","COPY",BODY,{"derivedFrom":makeQuery(id+"F5.opPattern","COPY",BODY,{"derivedFrom":makeQuery(id+"F4.opPattern","COPY",BODY,{"derivedFrom":makeQuery(id+"F1.opRevolve","SWEPT_BODY",BODY,{"disambiguationData":[OSD([sQuery(id+"F0.wireOp",EDGE,"E1")])]}),"instanceName":"1"}),"instanceName":"1"}),"instanceName":"1"}),"instanceName":"1"}),"instanceName":"1"});
            var Q921;
            Q921=makeQuery(id+"F12.opPattern","COPY",BODY,{"derivedFrom":makeQuery(id+"F9.opPattern","COPY",BODY,{"derivedFrom":makeQuery(id+"F8.opPattern","COPY",BODY,{"derivedFrom":makeQuery(id+"F5.opPattern","COPY",BODY,{"derivedFrom":makeQuery(id+"F4.opPattern","COPY",BODY,{"derivedFrom":makeQuery(id+"F2.opPattern","COPY",BODY,{"derivedFrom":makeQuery(id+"F1.opRevolve","SWEPT_BODY",BODY,{"disambiguationData":[OSD([sQuery(id+"F0.wireOp",EDGE,"E1")])]}),"instanceName":"1"}),"instanceName":"1"}),"instanceName":"1"}),"instanceName":"1"}),"instanceName":"1"}),"instanceName":"1"});
            var Q922;
            Q922=makeQuery(id+"F12.opPattern","COPY",BODY,{"derivedFrom":makeQuery(id+"F9.opPattern","COPY",BODY,{"derivedFrom":makeQuery(id+"F8.opPattern","COPY",BODY,{"derivedFrom":makeQuery(id+"F5.opPattern","COPY",BODY,{"derivedFrom":makeQuery(id+"F4.opPattern","COPY",BODY,{"derivedFrom":makeQuery(id+"F3.opPattern","COPY",BODY,{"derivedFrom":makeQuery(id+"F2.opPattern","COPY",BODY,{"derivedFrom":makeQuery(id+"F1.opRevolve","SWEPT_BODY",BODY,{"disambiguationData":[OSD([sQuery(id+"F0.wireOp",EDGE,"E1")])]}),"instanceName":"1"}),"instanceName":"1"}),"instanceName":"1"}),"instanceName":"1"}),"instanceName":"1"}),"instanceName":"1"}),"instanceName":"1"});
            var Q923;
            Q923=makeQuery(id+"F12.opPattern","COPY",BODY,{"derivedFrom":makeQuery(id+"F9.opPattern","COPY",BODY,{"derivedFrom":makeQuery(id+"F8.opPattern","COPY",BODY,{"derivedFrom":makeQuery(id+"F6.opPattern","COPY",BODY,{"derivedFrom":makeQuery(id+"F1.opRevolve","SWEPT_BODY",BODY,{"disambiguationData":[OSD([sQuery(id+"F0.wireOp",EDGE,"E1")])]}),"instanceName":"1"}),"instanceName":"1"}),"instanceName":"1"}),"instanceName":"1"});
            var Q924;
            Q924=makeQuery(id+"F12.opPattern","COPY",BODY,{"derivedFrom":makeQuery(id+"F9.opPattern","COPY",BODY,{"derivedFrom":makeQuery(id+"F8.opPattern","COPY",BODY,{"derivedFrom":makeQuery(id+"F6.opPattern","COPY",BODY,{"derivedFrom":makeQuery(id+"F2.opPattern","COPY",BODY,{"derivedFrom":makeQuery(id+"F1.opRevolve","SWEPT_BODY",BODY,{"disambiguationData":[OSD([sQuery(id+"F0.wireOp",EDGE,"E1")])]}),"instanceName":"1"}),"instanceName":"1"}),"instanceName":"1"}),"instanceName":"1"}),"instanceName":"1"});
            var Q925;
            Q925=makeQuery(id+"F12.opPattern","COPY",BODY,{"derivedFrom":makeQuery(id+"F9.opPattern","COPY",BODY,{"derivedFrom":makeQuery(id+"F8.opPattern","COPY",BODY,{"derivedFrom":makeQuery(id+"F6.opPattern","COPY",BODY,{"derivedFrom":makeQuery(id+"F3.opPattern","COPY",BODY,{"derivedFrom":makeQuery(id+"F2.opPattern","COPY",BODY,{"derivedFrom":makeQuery(id+"F1.opRevolve","SWEPT_BODY",BODY,{"disambiguationData":[OSD([sQuery(id+"F0.wireOp",EDGE,"E1")])]}),"instanceName":"1"}),"instanceName":"1"}),"instanceName":"1"}),"instanceName":"1"}),"instanceName":"1"}),"instanceName":"1"});
            var Q926;
            Q926=makeQuery(id+"F12.opPattern","COPY",BODY,{"derivedFrom":makeQuery(id+"F9.opPattern","COPY",BODY,{"derivedFrom":makeQuery(id+"F8.opPattern","COPY",BODY,{"derivedFrom":makeQuery(id+"F6.opPattern","COPY",BODY,{"derivedFrom":makeQuery(id+"F4.opPattern","COPY",BODY,{"derivedFrom":makeQuery(id+"F1.opRevolve","SWEPT_BODY",BODY,{"disambiguationData":[OSD([sQuery(id+"F0.wireOp",EDGE,"E1")])]}),"instanceName":"1"}),"instanceName":"1"}),"instanceName":"1"}),"instanceName":"1"}),"instanceName":"1"});
            var Q927;
            Q927=makeQuery(id+"F12.opPattern","COPY",BODY,{"derivedFrom":makeQuery(id+"F9.opPattern","COPY",BODY,{"derivedFrom":makeQuery(id+"F8.opPattern","COPY",BODY,{"derivedFrom":makeQuery(id+"F6.opPattern","COPY",BODY,{"derivedFrom":makeQuery(id+"F4.opPattern","COPY",BODY,{"derivedFrom":makeQuery(id+"F2.opPattern","COPY",BODY,{"derivedFrom":makeQuery(id+"F1.opRevolve","SWEPT_BODY",BODY,{"disambiguationData":[OSD([sQuery(id+"F0.wireOp",EDGE,"E1")])]}),"instanceName":"1"}),"instanceName":"1"}),"instanceName":"1"}),"instanceName":"1"}),"instanceName":"1"}),"instanceName":"1"});
            var Q928;
            Q928=makeQuery(id+"F12.opPattern","COPY",BODY,{"derivedFrom":makeQuery(id+"F9.opPattern","COPY",BODY,{"derivedFrom":makeQuery(id+"F8.opPattern","COPY",BODY,{"derivedFrom":makeQuery(id+"F6.opPattern","COPY",BODY,{"derivedFrom":makeQuery(id+"F4.opPattern","COPY",BODY,{"derivedFrom":makeQuery(id+"F3.opPattern","COPY",BODY,{"derivedFrom":makeQuery(id+"F2.opPattern","COPY",BODY,{"derivedFrom":makeQuery(id+"F1.opRevolve","SWEPT_BODY",BODY,{"disambiguationData":[OSD([sQuery(id+"F0.wireOp",EDGE,"E1")])]}),"instanceName":"1"}),"instanceName":"1"}),"instanceName":"1"}),"instanceName":"1"}),"instanceName":"1"}),"instanceName":"1"}),"instanceName":"1"});
            var Q929;
            Q929=makeQuery(id+"F12.opPattern","COPY",BODY,{"derivedFrom":makeQuery(id+"F9.opPattern","COPY",BODY,{"derivedFrom":makeQuery(id+"F8.opPattern","COPY",BODY,{"derivedFrom":makeQuery(id+"F6.opPattern","COPY",BODY,{"derivedFrom":makeQuery(id+"F5.opPattern","COPY",BODY,{"derivedFrom":makeQuery(id+"F1.opRevolve","SWEPT_BODY",BODY,{"disambiguationData":[OSD([sQuery(id+"F0.wireOp",EDGE,"E1")])]}),"instanceName":"1"}),"instanceName":"1"}),"instanceName":"1"}),"instanceName":"1"}),"instanceName":"1"});
            var Q930;
            Q930=makeQuery(id+"F12.opPattern","COPY",BODY,{"derivedFrom":makeQuery(id+"F9.opPattern","COPY",BODY,{"derivedFrom":makeQuery(id+"F8.opPattern","COPY",BODY,{"derivedFrom":makeQuery(id+"F6.opPattern","COPY",BODY,{"derivedFrom":makeQuery(id+"F5.opPattern","COPY",BODY,{"derivedFrom":makeQuery(id+"F2.opPattern","COPY",BODY,{"derivedFrom":makeQuery(id+"F1.opRevolve","SWEPT_BODY",BODY,{"disambiguationData":[OSD([sQuery(id+"F0.wireOp",EDGE,"E1")])]}),"instanceName":"1"}),"instanceName":"1"}),"instanceName":"1"}),"instanceName":"1"}),"instanceName":"1"}),"instanceName":"1"});
            var Q931;
            Q931=makeQuery(id+"F12.opPattern","COPY",BODY,{"derivedFrom":makeQuery(id+"F9.opPattern","COPY",BODY,{"derivedFrom":makeQuery(id+"F8.opPattern","COPY",BODY,{"derivedFrom":makeQuery(id+"F6.opPattern","COPY",BODY,{"derivedFrom":makeQuery(id+"F5.opPattern","COPY",BODY,{"derivedFrom":makeQuery(id+"F3.opPattern","COPY",BODY,{"derivedFrom":makeQuery(id+"F2.opPattern","COPY",BODY,{"derivedFrom":makeQuery(id+"F1.opRevolve","SWEPT_BODY",BODY,{"disambiguationData":[OSD([sQuery(id+"F0.wireOp",EDGE,"E1")])]}),"instanceName":"1"}),"instanceName":"1"}),"instanceName":"1"}),"instanceName":"1"}),"instanceName":"1"}),"instanceName":"1"}),"instanceName":"1"});
            var Q932;
            Q932=makeQuery(id+"F12.opPattern","COPY",BODY,{"derivedFrom":makeQuery(id+"F9.opPattern","COPY",BODY,{"derivedFrom":makeQuery(id+"F8.opPattern","COPY",BODY,{"derivedFrom":makeQuery(id+"F6.opPattern","COPY",BODY,{"derivedFrom":makeQuery(id+"F5.opPattern","COPY",BODY,{"derivedFrom":makeQuery(id+"F4.opPattern","COPY",BODY,{"derivedFrom":makeQuery(id+"F1.opRevolve","SWEPT_BODY",BODY,{"disambiguationData":[OSD([sQuery(id+"F0.wireOp",EDGE,"E1")])]}),"instanceName":"1"}),"instanceName":"1"}),"instanceName":"1"}),"instanceName":"1"}),"instanceName":"1"}),"instanceName":"1"});
            var Q933;
            Q933=makeQuery(id+"F12.opPattern","COPY",BODY,{"derivedFrom":makeQuery(id+"F9.opPattern","COPY",BODY,{"derivedFrom":makeQuery(id+"F8.opPattern","COPY",BODY,{"derivedFrom":makeQuery(id+"F6.opPattern","COPY",BODY,{"derivedFrom":makeQuery(id+"F5.opPattern","COPY",BODY,{"derivedFrom":makeQuery(id+"F4.opPattern","COPY",BODY,{"derivedFrom":makeQuery(id+"F2.opPattern","COPY",BODY,{"derivedFrom":makeQuery(id+"F1.opRevolve","SWEPT_BODY",BODY,{"disambiguationData":[OSD([sQuery(id+"F0.wireOp",EDGE,"E1")])]}),"instanceName":"1"}),"instanceName":"1"}),"instanceName":"1"}),"instanceName":"1"}),"instanceName":"1"}),"instanceName":"1"}),"instanceName":"1"});
            var Q934;
            Q934=makeQuery(id+"F12.opPattern","COPY",BODY,{"derivedFrom":makeQuery(id+"F9.opPattern","COPY",BODY,{"derivedFrom":makeQuery(id+"F8.opPattern","COPY",BODY,{"derivedFrom":makeQuery(id+"F6.opPattern","COPY",BODY,{"derivedFrom":makeQuery(id+"F5.opPattern","COPY",BODY,{"derivedFrom":makeQuery(id+"F4.opPattern","COPY",BODY,{"derivedFrom":makeQuery(id+"F3.opPattern","COPY",BODY,{"derivedFrom":makeQuery(id+"F2.opPattern","COPY",BODY,{"derivedFrom":makeQuery(id+"F1.opRevolve","SWEPT_BODY",BODY,{"disambiguationData":[OSD([sQuery(id+"F0.wireOp",EDGE,"E1")])]}),"instanceName":"1"}),"instanceName":"1"}),"instanceName":"1"}),"instanceName":"1"}),"instanceName":"1"}),"instanceName":"1"}),"instanceName":"1"}),"instanceName":"1"});
            var Q935;
            Q935=makeQuery(id+"F12.opPattern","COPY",BODY,{"derivedFrom":makeQuery(id+"F9.opPattern","COPY",BODY,{"derivedFrom":makeQuery(id+"F8.opPattern","COPY",BODY,{"derivedFrom":makeQuery(id+"F7.opPattern","COPY",BODY,{"derivedFrom":makeQuery(id+"F1.opRevolve","SWEPT_BODY",BODY,{"disambiguationData":[OSD([sQuery(id+"F0.wireOp",EDGE,"E1")])]}),"instanceName":"1"}),"instanceName":"1"}),"instanceName":"1"}),"instanceName":"1"});
            var Q936;
            Q936=makeQuery(id+"F12.opPattern","COPY",BODY,{"derivedFrom":makeQuery(id+"F9.opPattern","COPY",BODY,{"derivedFrom":makeQuery(id+"F8.opPattern","COPY",BODY,{"derivedFrom":makeQuery(id+"F7.opPattern","COPY",BODY,{"derivedFrom":makeQuery(id+"F2.opPattern","COPY",BODY,{"derivedFrom":makeQuery(id+"F1.opRevolve","SWEPT_BODY",BODY,{"disambiguationData":[OSD([sQuery(id+"F0.wireOp",EDGE,"E1")])]}),"instanceName":"1"}),"instanceName":"1"}),"instanceName":"1"}),"instanceName":"1"}),"instanceName":"1"});
            var Q937;
            Q937=makeQuery(id+"F12.opPattern","COPY",BODY,{"derivedFrom":makeQuery(id+"F9.opPattern","COPY",BODY,{"derivedFrom":makeQuery(id+"F8.opPattern","COPY",BODY,{"derivedFrom":makeQuery(id+"F7.opPattern","COPY",BODY,{"derivedFrom":makeQuery(id+"F3.opPattern","COPY",BODY,{"derivedFrom":makeQuery(id+"F2.opPattern","COPY",BODY,{"derivedFrom":makeQuery(id+"F1.opRevolve","SWEPT_BODY",BODY,{"disambiguationData":[OSD([sQuery(id+"F0.wireOp",EDGE,"E1")])]}),"instanceName":"1"}),"instanceName":"1"}),"instanceName":"1"}),"instanceName":"1"}),"instanceName":"1"}),"instanceName":"1"});
            var Q938;
            Q938=makeQuery(id+"F12.opPattern","COPY",BODY,{"derivedFrom":makeQuery(id+"F9.opPattern","COPY",BODY,{"derivedFrom":makeQuery(id+"F8.opPattern","COPY",BODY,{"derivedFrom":makeQuery(id+"F7.opPattern","COPY",BODY,{"derivedFrom":makeQuery(id+"F4.opPattern","COPY",BODY,{"derivedFrom":makeQuery(id+"F1.opRevolve","SWEPT_BODY",BODY,{"disambiguationData":[OSD([sQuery(id+"F0.wireOp",EDGE,"E1")])]}),"instanceName":"1"}),"instanceName":"1"}),"instanceName":"1"}),"instanceName":"1"}),"instanceName":"1"});
            var Q939;
            Q939=makeQuery(id+"F12.opPattern","COPY",BODY,{"derivedFrom":makeQuery(id+"F9.opPattern","COPY",BODY,{"derivedFrom":makeQuery(id+"F8.opPattern","COPY",BODY,{"derivedFrom":makeQuery(id+"F7.opPattern","COPY",BODY,{"derivedFrom":makeQuery(id+"F4.opPattern","COPY",BODY,{"derivedFrom":makeQuery(id+"F2.opPattern","COPY",BODY,{"derivedFrom":makeQuery(id+"F1.opRevolve","SWEPT_BODY",BODY,{"disambiguationData":[OSD([sQuery(id+"F0.wireOp",EDGE,"E1")])]}),"instanceName":"1"}),"instanceName":"1"}),"instanceName":"1"}),"instanceName":"1"}),"instanceName":"1"}),"instanceName":"1"});
            var Q940;
            Q940=makeQuery(id+"F12.opPattern","COPY",BODY,{"derivedFrom":makeQuery(id+"F9.opPattern","COPY",BODY,{"derivedFrom":makeQuery(id+"F8.opPattern","COPY",BODY,{"derivedFrom":makeQuery(id+"F7.opPattern","COPY",BODY,{"derivedFrom":makeQuery(id+"F4.opPattern","COPY",BODY,{"derivedFrom":makeQuery(id+"F3.opPattern","COPY",BODY,{"derivedFrom":makeQuery(id+"F2.opPattern","COPY",BODY,{"derivedFrom":makeQuery(id+"F1.opRevolve","SWEPT_BODY",BODY,{"disambiguationData":[OSD([sQuery(id+"F0.wireOp",EDGE,"E1")])]}),"instanceName":"1"}),"instanceName":"1"}),"instanceName":"1"}),"instanceName":"1"}),"instanceName":"1"}),"instanceName":"1"}),"instanceName":"1"});
            var Q941;
            Q941=makeQuery(id+"F12.opPattern","COPY",BODY,{"derivedFrom":makeQuery(id+"F9.opPattern","COPY",BODY,{"derivedFrom":makeQuery(id+"F8.opPattern","COPY",BODY,{"derivedFrom":makeQuery(id+"F7.opPattern","COPY",BODY,{"derivedFrom":makeQuery(id+"F5.opPattern","COPY",BODY,{"derivedFrom":makeQuery(id+"F1.opRevolve","SWEPT_BODY",BODY,{"disambiguationData":[OSD([sQuery(id+"F0.wireOp",EDGE,"E1")])]}),"instanceName":"1"}),"instanceName":"1"}),"instanceName":"1"}),"instanceName":"1"}),"instanceName":"1"});
            var Q942;
            Q942=makeQuery(id+"F12.opPattern","COPY",BODY,{"derivedFrom":makeQuery(id+"F9.opPattern","COPY",BODY,{"derivedFrom":makeQuery(id+"F8.opPattern","COPY",BODY,{"derivedFrom":makeQuery(id+"F7.opPattern","COPY",BODY,{"derivedFrom":makeQuery(id+"F5.opPattern","COPY",BODY,{"derivedFrom":makeQuery(id+"F2.opPattern","COPY",BODY,{"derivedFrom":makeQuery(id+"F1.opRevolve","SWEPT_BODY",BODY,{"disambiguationData":[OSD([sQuery(id+"F0.wireOp",EDGE,"E1")])]}),"instanceName":"1"}),"instanceName":"1"}),"instanceName":"1"}),"instanceName":"1"}),"instanceName":"1"}),"instanceName":"1"});
            var Q943;
            Q943=makeQuery(id+"F12.opPattern","COPY",BODY,{"derivedFrom":makeQuery(id+"F9.opPattern","COPY",BODY,{"derivedFrom":makeQuery(id+"F8.opPattern","COPY",BODY,{"derivedFrom":makeQuery(id+"F7.opPattern","COPY",BODY,{"derivedFrom":makeQuery(id+"F5.opPattern","COPY",BODY,{"derivedFrom":makeQuery(id+"F3.opPattern","COPY",BODY,{"derivedFrom":makeQuery(id+"F2.opPattern","COPY",BODY,{"derivedFrom":makeQuery(id+"F1.opRevolve","SWEPT_BODY",BODY,{"disambiguationData":[OSD([sQuery(id+"F0.wireOp",EDGE,"E1")])]}),"instanceName":"1"}),"instanceName":"1"}),"instanceName":"1"}),"instanceName":"1"}),"instanceName":"1"}),"instanceName":"1"}),"instanceName":"1"});
            var Q944;
            Q944=makeQuery(id+"F12.opPattern","COPY",BODY,{"derivedFrom":makeQuery(id+"F9.opPattern","COPY",BODY,{"derivedFrom":makeQuery(id+"F8.opPattern","COPY",BODY,{"derivedFrom":makeQuery(id+"F7.opPattern","COPY",BODY,{"derivedFrom":makeQuery(id+"F5.opPattern","COPY",BODY,{"derivedFrom":makeQuery(id+"F4.opPattern","COPY",BODY,{"derivedFrom":makeQuery(id+"F1.opRevolve","SWEPT_BODY",BODY,{"disambiguationData":[OSD([sQuery(id+"F0.wireOp",EDGE,"E1")])]}),"instanceName":"1"}),"instanceName":"1"}),"instanceName":"1"}),"instanceName":"1"}),"instanceName":"1"}),"instanceName":"1"});
            var Q945;
            Q945=makeQuery(id+"F12.opPattern","COPY",BODY,{"derivedFrom":makeQuery(id+"F9.opPattern","COPY",BODY,{"derivedFrom":makeQuery(id+"F8.opPattern","COPY",BODY,{"derivedFrom":makeQuery(id+"F7.opPattern","COPY",BODY,{"derivedFrom":makeQuery(id+"F5.opPattern","COPY",BODY,{"derivedFrom":makeQuery(id+"F4.opPattern","COPY",BODY,{"derivedFrom":makeQuery(id+"F2.opPattern","COPY",BODY,{"derivedFrom":makeQuery(id+"F1.opRevolve","SWEPT_BODY",BODY,{"disambiguationData":[OSD([sQuery(id+"F0.wireOp",EDGE,"E1")])]}),"instanceName":"1"}),"instanceName":"1"}),"instanceName":"1"}),"instanceName":"1"}),"instanceName":"1"}),"instanceName":"1"}),"instanceName":"1"});
            var Q946;
            Q946=makeQuery(id+"F12.opPattern","COPY",BODY,{"derivedFrom":makeQuery(id+"F9.opPattern","COPY",BODY,{"derivedFrom":makeQuery(id+"F8.opPattern","COPY",BODY,{"derivedFrom":makeQuery(id+"F7.opPattern","COPY",BODY,{"derivedFrom":makeQuery(id+"F5.opPattern","COPY",BODY,{"derivedFrom":makeQuery(id+"F4.opPattern","COPY",BODY,{"derivedFrom":makeQuery(id+"F3.opPattern","COPY",BODY,{"derivedFrom":makeQuery(id+"F2.opPattern","COPY",BODY,{"derivedFrom":makeQuery(id+"F1.opRevolve","SWEPT_BODY",BODY,{"disambiguationData":[OSD([sQuery(id+"F0.wireOp",EDGE,"E1")])]}),"instanceName":"1"}),"instanceName":"1"}),"instanceName":"1"}),"instanceName":"1"}),"instanceName":"1"}),"instanceName":"1"}),"instanceName":"1"}),"instanceName":"1"});
            var Q947;
            Q947=makeQuery(id+"F12.opPattern","COPY",BODY,{"derivedFrom":makeQuery(id+"F9.opPattern","COPY",BODY,{"derivedFrom":makeQuery(id+"F8.opPattern","COPY",BODY,{"derivedFrom":makeQuery(id+"F7.opPattern","COPY",BODY,{"derivedFrom":makeQuery(id+"F6.opPattern","COPY",BODY,{"derivedFrom":makeQuery(id+"F1.opRevolve","SWEPT_BODY",BODY,{"disambiguationData":[OSD([sQuery(id+"F0.wireOp",EDGE,"E1")])]}),"instanceName":"1"}),"instanceName":"1"}),"instanceName":"1"}),"instanceName":"1"}),"instanceName":"1"});
            var Q948;
            Q948=makeQuery(id+"F12.opPattern","COPY",BODY,{"derivedFrom":makeQuery(id+"F9.opPattern","COPY",BODY,{"derivedFrom":makeQuery(id+"F8.opPattern","COPY",BODY,{"derivedFrom":makeQuery(id+"F7.opPattern","COPY",BODY,{"derivedFrom":makeQuery(id+"F6.opPattern","COPY",BODY,{"derivedFrom":makeQuery(id+"F2.opPattern","COPY",BODY,{"derivedFrom":makeQuery(id+"F1.opRevolve","SWEPT_BODY",BODY,{"disambiguationData":[OSD([sQuery(id+"F0.wireOp",EDGE,"E1")])]}),"instanceName":"1"}),"instanceName":"1"}),"instanceName":"1"}),"instanceName":"1"}),"instanceName":"1"}),"instanceName":"1"});
            var Q949;
            Q949=makeQuery(id+"F12.opPattern","COPY",BODY,{"derivedFrom":makeQuery(id+"F9.opPattern","COPY",BODY,{"derivedFrom":makeQuery(id+"F8.opPattern","COPY",BODY,{"derivedFrom":makeQuery(id+"F7.opPattern","COPY",BODY,{"derivedFrom":makeQuery(id+"F6.opPattern","COPY",BODY,{"derivedFrom":makeQuery(id+"F3.opPattern","COPY",BODY,{"derivedFrom":makeQuery(id+"F2.opPattern","COPY",BODY,{"derivedFrom":makeQuery(id+"F1.opRevolve","SWEPT_BODY",BODY,{"disambiguationData":[OSD([sQuery(id+"F0.wireOp",EDGE,"E1")])]}),"instanceName":"1"}),"instanceName":"1"}),"instanceName":"1"}),"instanceName":"1"}),"instanceName":"1"}),"instanceName":"1"}),"instanceName":"1"});
            var Q950;
            Q950=makeQuery(id+"F12.opPattern","COPY",BODY,{"derivedFrom":makeQuery(id+"F9.opPattern","COPY",BODY,{"derivedFrom":makeQuery(id+"F8.opPattern","COPY",BODY,{"derivedFrom":makeQuery(id+"F7.opPattern","COPY",BODY,{"derivedFrom":makeQuery(id+"F6.opPattern","COPY",BODY,{"derivedFrom":makeQuery(id+"F4.opPattern","COPY",BODY,{"derivedFrom":makeQuery(id+"F1.opRevolve","SWEPT_BODY",BODY,{"disambiguationData":[OSD([sQuery(id+"F0.wireOp",EDGE,"E1")])]}),"instanceName":"1"}),"instanceName":"1"}),"instanceName":"1"}),"instanceName":"1"}),"instanceName":"1"}),"instanceName":"1"});
            var Q951;
            Q951=makeQuery(id+"F12.opPattern","COPY",BODY,{"derivedFrom":makeQuery(id+"F9.opPattern","COPY",BODY,{"derivedFrom":makeQuery(id+"F8.opPattern","COPY",BODY,{"derivedFrom":makeQuery(id+"F7.opPattern","COPY",BODY,{"derivedFrom":makeQuery(id+"F6.opPattern","COPY",BODY,{"derivedFrom":makeQuery(id+"F4.opPattern","COPY",BODY,{"derivedFrom":makeQuery(id+"F2.opPattern","COPY",BODY,{"derivedFrom":makeQuery(id+"F1.opRevolve","SWEPT_BODY",BODY,{"disambiguationData":[OSD([sQuery(id+"F0.wireOp",EDGE,"E1")])]}),"instanceName":"1"}),"instanceName":"1"}),"instanceName":"1"}),"instanceName":"1"}),"instanceName":"1"}),"instanceName":"1"}),"instanceName":"1"});
            var Q952;
            Q952=makeQuery(id+"F12.opPattern","COPY",BODY,{"derivedFrom":makeQuery(id+"F9.opPattern","COPY",BODY,{"derivedFrom":makeQuery(id+"F8.opPattern","COPY",BODY,{"derivedFrom":makeQuery(id+"F7.opPattern","COPY",BODY,{"derivedFrom":makeQuery(id+"F6.opPattern","COPY",BODY,{"derivedFrom":makeQuery(id+"F4.opPattern","COPY",BODY,{"derivedFrom":makeQuery(id+"F3.opPattern","COPY",BODY,{"derivedFrom":makeQuery(id+"F2.opPattern","COPY",BODY,{"derivedFrom":makeQuery(id+"F1.opRevolve","SWEPT_BODY",BODY,{"disambiguationData":[OSD([sQuery(id+"F0.wireOp",EDGE,"E1")])]}),"instanceName":"1"}),"instanceName":"1"}),"instanceName":"1"}),"instanceName":"1"}),"instanceName":"1"}),"instanceName":"1"}),"instanceName":"1"}),"instanceName":"1"});
            var Q953;
            Q953=makeQuery(id+"F12.opPattern","COPY",BODY,{"derivedFrom":makeQuery(id+"F9.opPattern","COPY",BODY,{"derivedFrom":makeQuery(id+"F8.opPattern","COPY",BODY,{"derivedFrom":makeQuery(id+"F7.opPattern","COPY",BODY,{"derivedFrom":makeQuery(id+"F6.opPattern","COPY",BODY,{"derivedFrom":makeQuery(id+"F5.opPattern","COPY",BODY,{"derivedFrom":makeQuery(id+"F1.opRevolve","SWEPT_BODY",BODY,{"disambiguationData":[OSD([sQuery(id+"F0.wireOp",EDGE,"E1")])]}),"instanceName":"1"}),"instanceName":"1"}),"instanceName":"1"}),"instanceName":"1"}),"instanceName":"1"}),"instanceName":"1"});
            var Q954;
            Q954=makeQuery(id+"F12.opPattern","COPY",BODY,{"derivedFrom":makeQuery(id+"F9.opPattern","COPY",BODY,{"derivedFrom":makeQuery(id+"F8.opPattern","COPY",BODY,{"derivedFrom":makeQuery(id+"F7.opPattern","COPY",BODY,{"derivedFrom":makeQuery(id+"F6.opPattern","COPY",BODY,{"derivedFrom":makeQuery(id+"F5.opPattern","COPY",BODY,{"derivedFrom":makeQuery(id+"F2.opPattern","COPY",BODY,{"derivedFrom":makeQuery(id+"F1.opRevolve","SWEPT_BODY",BODY,{"disambiguationData":[OSD([sQuery(id+"F0.wireOp",EDGE,"E1")])]}),"instanceName":"1"}),"instanceName":"1"}),"instanceName":"1"}),"instanceName":"1"}),"instanceName":"1"}),"instanceName":"1"}),"instanceName":"1"});
            var Q955;
            Q955=makeQuery(id+"F12.opPattern","COPY",BODY,{"derivedFrom":makeQuery(id+"F9.opPattern","COPY",BODY,{"derivedFrom":makeQuery(id+"F8.opPattern","COPY",BODY,{"derivedFrom":makeQuery(id+"F7.opPattern","COPY",BODY,{"derivedFrom":makeQuery(id+"F6.opPattern","COPY",BODY,{"derivedFrom":makeQuery(id+"F5.opPattern","COPY",BODY,{"derivedFrom":makeQuery(id+"F3.opPattern","COPY",BODY,{"derivedFrom":makeQuery(id+"F2.opPattern","COPY",BODY,{"derivedFrom":makeQuery(id+"F1.opRevolve","SWEPT_BODY",BODY,{"disambiguationData":[OSD([sQuery(id+"F0.wireOp",EDGE,"E1")])]}),"instanceName":"1"}),"instanceName":"1"}),"instanceName":"1"}),"instanceName":"1"}),"instanceName":"1"}),"instanceName":"1"}),"instanceName":"1"}),"instanceName":"1"});
            var Q956;
            Q956=makeQuery(id+"F12.opPattern","COPY",BODY,{"derivedFrom":makeQuery(id+"F9.opPattern","COPY",BODY,{"derivedFrom":makeQuery(id+"F8.opPattern","COPY",BODY,{"derivedFrom":makeQuery(id+"F7.opPattern","COPY",BODY,{"derivedFrom":makeQuery(id+"F6.opPattern","COPY",BODY,{"derivedFrom":makeQuery(id+"F5.opPattern","COPY",BODY,{"derivedFrom":makeQuery(id+"F4.opPattern","COPY",BODY,{"derivedFrom":makeQuery(id+"F1.opRevolve","SWEPT_BODY",BODY,{"disambiguationData":[OSD([sQuery(id+"F0.wireOp",EDGE,"E1")])]}),"instanceName":"1"}),"instanceName":"1"}),"instanceName":"1"}),"instanceName":"1"}),"instanceName":"1"}),"instanceName":"1"}),"instanceName":"1"});
            var Q957;
            Q957=makeQuery(id+"F12.opPattern","COPY",BODY,{"derivedFrom":makeQuery(id+"F9.opPattern","COPY",BODY,{"derivedFrom":makeQuery(id+"F8.opPattern","COPY",BODY,{"derivedFrom":makeQuery(id+"F7.opPattern","COPY",BODY,{"derivedFrom":makeQuery(id+"F6.opPattern","COPY",BODY,{"derivedFrom":makeQuery(id+"F5.opPattern","COPY",BODY,{"derivedFrom":makeQuery(id+"F4.opPattern","COPY",BODY,{"derivedFrom":makeQuery(id+"F2.opPattern","COPY",BODY,{"derivedFrom":makeQuery(id+"F1.opRevolve","SWEPT_BODY",BODY,{"disambiguationData":[OSD([sQuery(id+"F0.wireOp",EDGE,"E1")])]}),"instanceName":"1"}),"instanceName":"1"}),"instanceName":"1"}),"instanceName":"1"}),"instanceName":"1"}),"instanceName":"1"}),"instanceName":"1"}),"instanceName":"1"});
            var Q958;
            Q958=makeQuery(id+"F12.opPattern","COPY",BODY,{"derivedFrom":makeQuery(id+"F9.opPattern","COPY",BODY,{"derivedFrom":makeQuery(id+"F8.opPattern","COPY",BODY,{"derivedFrom":makeQuery(id+"F7.opPattern","COPY",BODY,{"derivedFrom":makeQuery(id+"F6.opPattern","COPY",BODY,{"derivedFrom":makeQuery(id+"F5.opPattern","COPY",BODY,{"derivedFrom":makeQuery(id+"F4.opPattern","COPY",BODY,{"derivedFrom":makeQuery(id+"F3.opPattern","COPY",BODY,{"derivedFrom":makeQuery(id+"F2.opPattern","COPY",BODY,{"derivedFrom":makeQuery(id+"F1.opRevolve","SWEPT_BODY",BODY,{"disambiguationData":[OSD([sQuery(id+"F0.wireOp",EDGE,"E1")])]}),"instanceName":"1"}),"instanceName":"1"}),"instanceName":"1"}),"instanceName":"1"}),"instanceName":"1"}),"instanceName":"1"}),"instanceName":"1"}),"instanceName":"1"}),"instanceName":"1"});
            var Q959;
            Q959=makeQuery(id+"F12.opPattern","COPY",BODY,{"derivedFrom":makeQuery(id+"F10.opPattern","COPY",BODY,{"derivedFrom":makeQuery(id+"F1.opRevolve","SWEPT_BODY",BODY,{"disambiguationData":[OSD([sQuery(id+"F0.wireOp",EDGE,"E1")])]}),"instanceName":"1"}),"instanceName":"1"});
            var Q960;
            Q960=makeQuery(id+"F12.opPattern","COPY",BODY,{"derivedFrom":makeQuery(id+"F10.opPattern","COPY",BODY,{"derivedFrom":makeQuery(id+"F2.opPattern","COPY",BODY,{"derivedFrom":makeQuery(id+"F1.opRevolve","SWEPT_BODY",BODY,{"disambiguationData":[OSD([sQuery(id+"F0.wireOp",EDGE,"E1")])]}),"instanceName":"1"}),"instanceName":"1"}),"instanceName":"1"});
            var Q961;
            Q961=makeQuery(id+"F12.opPattern","COPY",BODY,{"derivedFrom":makeQuery(id+"F10.opPattern","COPY",BODY,{"derivedFrom":makeQuery(id+"F3.opPattern","COPY",BODY,{"derivedFrom":makeQuery(id+"F2.opPattern","COPY",BODY,{"derivedFrom":makeQuery(id+"F1.opRevolve","SWEPT_BODY",BODY,{"disambiguationData":[OSD([sQuery(id+"F0.wireOp",EDGE,"E1")])]}),"instanceName":"1"}),"instanceName":"1"}),"instanceName":"1"}),"instanceName":"1"});
            var Q962;
            Q962=makeQuery(id+"F12.opPattern","COPY",BODY,{"derivedFrom":makeQuery(id+"F10.opPattern","COPY",BODY,{"derivedFrom":makeQuery(id+"F4.opPattern","COPY",BODY,{"derivedFrom":makeQuery(id+"F1.opRevolve","SWEPT_BODY",BODY,{"disambiguationData":[OSD([sQuery(id+"F0.wireOp",EDGE,"E1")])]}),"instanceName":"1"}),"instanceName":"1"}),"instanceName":"1"});
            var Q963;
            Q963=makeQuery(id+"F12.opPattern","COPY",BODY,{"derivedFrom":makeQuery(id+"F10.opPattern","COPY",BODY,{"derivedFrom":makeQuery(id+"F4.opPattern","COPY",BODY,{"derivedFrom":makeQuery(id+"F2.opPattern","COPY",BODY,{"derivedFrom":makeQuery(id+"F1.opRevolve","SWEPT_BODY",BODY,{"disambiguationData":[OSD([sQuery(id+"F0.wireOp",EDGE,"E1")])]}),"instanceName":"1"}),"instanceName":"1"}),"instanceName":"1"}),"instanceName":"1"});
            var Q964;
            Q964=makeQuery(id+"F12.opPattern","COPY",BODY,{"derivedFrom":makeQuery(id+"F10.opPattern","COPY",BODY,{"derivedFrom":makeQuery(id+"F4.opPattern","COPY",BODY,{"derivedFrom":makeQuery(id+"F3.opPattern","COPY",BODY,{"derivedFrom":makeQuery(id+"F2.opPattern","COPY",BODY,{"derivedFrom":makeQuery(id+"F1.opRevolve","SWEPT_BODY",BODY,{"disambiguationData":[OSD([sQuery(id+"F0.wireOp",EDGE,"E1")])]}),"instanceName":"1"}),"instanceName":"1"}),"instanceName":"1"}),"instanceName":"1"}),"instanceName":"1"});
            var Q965;
            Q965=makeQuery(id+"F12.opPattern","COPY",BODY,{"derivedFrom":makeQuery(id+"F10.opPattern","COPY",BODY,{"derivedFrom":makeQuery(id+"F5.opPattern","COPY",BODY,{"derivedFrom":makeQuery(id+"F1.opRevolve","SWEPT_BODY",BODY,{"disambiguationData":[OSD([sQuery(id+"F0.wireOp",EDGE,"E1")])]}),"instanceName":"1"}),"instanceName":"1"}),"instanceName":"1"});
            var Q966;
            Q966=makeQuery(id+"F12.opPattern","COPY",BODY,{"derivedFrom":makeQuery(id+"F10.opPattern","COPY",BODY,{"derivedFrom":makeQuery(id+"F5.opPattern","COPY",BODY,{"derivedFrom":makeQuery(id+"F2.opPattern","COPY",BODY,{"derivedFrom":makeQuery(id+"F1.opRevolve","SWEPT_BODY",BODY,{"disambiguationData":[OSD([sQuery(id+"F0.wireOp",EDGE,"E1")])]}),"instanceName":"1"}),"instanceName":"1"}),"instanceName":"1"}),"instanceName":"1"});
            var Q967;
            Q967=makeQuery(id+"F12.opPattern","COPY",BODY,{"derivedFrom":makeQuery(id+"F10.opPattern","COPY",BODY,{"derivedFrom":makeQuery(id+"F5.opPattern","COPY",BODY,{"derivedFrom":makeQuery(id+"F3.opPattern","COPY",BODY,{"derivedFrom":makeQuery(id+"F2.opPattern","COPY",BODY,{"derivedFrom":makeQuery(id+"F1.opRevolve","SWEPT_BODY",BODY,{"disambiguationData":[OSD([sQuery(id+"F0.wireOp",EDGE,"E1")])]}),"instanceName":"1"}),"instanceName":"1"}),"instanceName":"1"}),"instanceName":"1"}),"instanceName":"1"});
            var Q968;
            Q968=makeQuery(id+"F12.opPattern","COPY",BODY,{"derivedFrom":makeQuery(id+"F10.opPattern","COPY",BODY,{"derivedFrom":makeQuery(id+"F5.opPattern","COPY",BODY,{"derivedFrom":makeQuery(id+"F4.opPattern","COPY",BODY,{"derivedFrom":makeQuery(id+"F1.opRevolve","SWEPT_BODY",BODY,{"disambiguationData":[OSD([sQuery(id+"F0.wireOp",EDGE,"E1")])]}),"instanceName":"1"}),"instanceName":"1"}),"instanceName":"1"}),"instanceName":"1"});
            var Q969;
            Q969=makeQuery(id+"F12.opPattern","COPY",BODY,{"derivedFrom":makeQuery(id+"F10.opPattern","COPY",BODY,{"derivedFrom":makeQuery(id+"F5.opPattern","COPY",BODY,{"derivedFrom":makeQuery(id+"F4.opPattern","COPY",BODY,{"derivedFrom":makeQuery(id+"F2.opPattern","COPY",BODY,{"derivedFrom":makeQuery(id+"F1.opRevolve","SWEPT_BODY",BODY,{"disambiguationData":[OSD([sQuery(id+"F0.wireOp",EDGE,"E1")])]}),"instanceName":"1"}),"instanceName":"1"}),"instanceName":"1"}),"instanceName":"1"}),"instanceName":"1"});
            var Q970;
            Q970=makeQuery(id+"F12.opPattern","COPY",BODY,{"derivedFrom":makeQuery(id+"F10.opPattern","COPY",BODY,{"derivedFrom":makeQuery(id+"F5.opPattern","COPY",BODY,{"derivedFrom":makeQuery(id+"F4.opPattern","COPY",BODY,{"derivedFrom":makeQuery(id+"F3.opPattern","COPY",BODY,{"derivedFrom":makeQuery(id+"F2.opPattern","COPY",BODY,{"derivedFrom":makeQuery(id+"F1.opRevolve","SWEPT_BODY",BODY,{"disambiguationData":[OSD([sQuery(id+"F0.wireOp",EDGE,"E1")])]}),"instanceName":"1"}),"instanceName":"1"}),"instanceName":"1"}),"instanceName":"1"}),"instanceName":"1"}),"instanceName":"1"});
            var Q971;
            Q971=makeQuery(id+"F12.opPattern","COPY",BODY,{"derivedFrom":makeQuery(id+"F10.opPattern","COPY",BODY,{"derivedFrom":makeQuery(id+"F6.opPattern","COPY",BODY,{"derivedFrom":makeQuery(id+"F1.opRevolve","SWEPT_BODY",BODY,{"disambiguationData":[OSD([sQuery(id+"F0.wireOp",EDGE,"E1")])]}),"instanceName":"1"}),"instanceName":"1"}),"instanceName":"1"});
            var Q972;
            Q972=makeQuery(id+"F12.opPattern","COPY",BODY,{"derivedFrom":makeQuery(id+"F10.opPattern","COPY",BODY,{"derivedFrom":makeQuery(id+"F6.opPattern","COPY",BODY,{"derivedFrom":makeQuery(id+"F2.opPattern","COPY",BODY,{"derivedFrom":makeQuery(id+"F1.opRevolve","SWEPT_BODY",BODY,{"disambiguationData":[OSD([sQuery(id+"F0.wireOp",EDGE,"E1")])]}),"instanceName":"1"}),"instanceName":"1"}),"instanceName":"1"}),"instanceName":"1"});
            var Q973;
            Q973=makeQuery(id+"F12.opPattern","COPY",BODY,{"derivedFrom":makeQuery(id+"F10.opPattern","COPY",BODY,{"derivedFrom":makeQuery(id+"F6.opPattern","COPY",BODY,{"derivedFrom":makeQuery(id+"F3.opPattern","COPY",BODY,{"derivedFrom":makeQuery(id+"F2.opPattern","COPY",BODY,{"derivedFrom":makeQuery(id+"F1.opRevolve","SWEPT_BODY",BODY,{"disambiguationData":[OSD([sQuery(id+"F0.wireOp",EDGE,"E1")])]}),"instanceName":"1"}),"instanceName":"1"}),"instanceName":"1"}),"instanceName":"1"}),"instanceName":"1"});
            var Q974;
            Q974=makeQuery(id+"F12.opPattern","COPY",BODY,{"derivedFrom":makeQuery(id+"F10.opPattern","COPY",BODY,{"derivedFrom":makeQuery(id+"F6.opPattern","COPY",BODY,{"derivedFrom":makeQuery(id+"F4.opPattern","COPY",BODY,{"derivedFrom":makeQuery(id+"F1.opRevolve","SWEPT_BODY",BODY,{"disambiguationData":[OSD([sQuery(id+"F0.wireOp",EDGE,"E1")])]}),"instanceName":"1"}),"instanceName":"1"}),"instanceName":"1"}),"instanceName":"1"});
            var Q975;
            Q975=makeQuery(id+"F12.opPattern","COPY",BODY,{"derivedFrom":makeQuery(id+"F10.opPattern","COPY",BODY,{"derivedFrom":makeQuery(id+"F6.opPattern","COPY",BODY,{"derivedFrom":makeQuery(id+"F4.opPattern","COPY",BODY,{"derivedFrom":makeQuery(id+"F2.opPattern","COPY",BODY,{"derivedFrom":makeQuery(id+"F1.opRevolve","SWEPT_BODY",BODY,{"disambiguationData":[OSD([sQuery(id+"F0.wireOp",EDGE,"E1")])]}),"instanceName":"1"}),"instanceName":"1"}),"instanceName":"1"}),"instanceName":"1"}),"instanceName":"1"});
            var Q976;
            Q976=makeQuery(id+"F12.opPattern","COPY",BODY,{"derivedFrom":makeQuery(id+"F10.opPattern","COPY",BODY,{"derivedFrom":makeQuery(id+"F6.opPattern","COPY",BODY,{"derivedFrom":makeQuery(id+"F4.opPattern","COPY",BODY,{"derivedFrom":makeQuery(id+"F3.opPattern","COPY",BODY,{"derivedFrom":makeQuery(id+"F2.opPattern","COPY",BODY,{"derivedFrom":makeQuery(id+"F1.opRevolve","SWEPT_BODY",BODY,{"disambiguationData":[OSD([sQuery(id+"F0.wireOp",EDGE,"E1")])]}),"instanceName":"1"}),"instanceName":"1"}),"instanceName":"1"}),"instanceName":"1"}),"instanceName":"1"}),"instanceName":"1"});
            var Q977;
            Q977=makeQuery(id+"F12.opPattern","COPY",BODY,{"derivedFrom":makeQuery(id+"F10.opPattern","COPY",BODY,{"derivedFrom":makeQuery(id+"F6.opPattern","COPY",BODY,{"derivedFrom":makeQuery(id+"F5.opPattern","COPY",BODY,{"derivedFrom":makeQuery(id+"F1.opRevolve","SWEPT_BODY",BODY,{"disambiguationData":[OSD([sQuery(id+"F0.wireOp",EDGE,"E1")])]}),"instanceName":"1"}),"instanceName":"1"}),"instanceName":"1"}),"instanceName":"1"});
            var Q978;
            Q978=makeQuery(id+"F12.opPattern","COPY",BODY,{"derivedFrom":makeQuery(id+"F10.opPattern","COPY",BODY,{"derivedFrom":makeQuery(id+"F6.opPattern","COPY",BODY,{"derivedFrom":makeQuery(id+"F5.opPattern","COPY",BODY,{"derivedFrom":makeQuery(id+"F2.opPattern","COPY",BODY,{"derivedFrom":makeQuery(id+"F1.opRevolve","SWEPT_BODY",BODY,{"disambiguationData":[OSD([sQuery(id+"F0.wireOp",EDGE,"E1")])]}),"instanceName":"1"}),"instanceName":"1"}),"instanceName":"1"}),"instanceName":"1"}),"instanceName":"1"});
            var Q979;
            Q979=makeQuery(id+"F12.opPattern","COPY",BODY,{"derivedFrom":makeQuery(id+"F10.opPattern","COPY",BODY,{"derivedFrom":makeQuery(id+"F6.opPattern","COPY",BODY,{"derivedFrom":makeQuery(id+"F5.opPattern","COPY",BODY,{"derivedFrom":makeQuery(id+"F3.opPattern","COPY",BODY,{"derivedFrom":makeQuery(id+"F2.opPattern","COPY",BODY,{"derivedFrom":makeQuery(id+"F1.opRevolve","SWEPT_BODY",BODY,{"disambiguationData":[OSD([sQuery(id+"F0.wireOp",EDGE,"E1")])]}),"instanceName":"1"}),"instanceName":"1"}),"instanceName":"1"}),"instanceName":"1"}),"instanceName":"1"}),"instanceName":"1"});
            var Q980;
            Q980=makeQuery(id+"F12.opPattern","COPY",BODY,{"derivedFrom":makeQuery(id+"F10.opPattern","COPY",BODY,{"derivedFrom":makeQuery(id+"F6.opPattern","COPY",BODY,{"derivedFrom":makeQuery(id+"F5.opPattern","COPY",BODY,{"derivedFrom":makeQuery(id+"F4.opPattern","COPY",BODY,{"derivedFrom":makeQuery(id+"F1.opRevolve","SWEPT_BODY",BODY,{"disambiguationData":[OSD([sQuery(id+"F0.wireOp",EDGE,"E1")])]}),"instanceName":"1"}),"instanceName":"1"}),"instanceName":"1"}),"instanceName":"1"}),"instanceName":"1"});
            var Q981;
            Q981=makeQuery(id+"F12.opPattern","COPY",BODY,{"derivedFrom":makeQuery(id+"F10.opPattern","COPY",BODY,{"derivedFrom":makeQuery(id+"F6.opPattern","COPY",BODY,{"derivedFrom":makeQuery(id+"F5.opPattern","COPY",BODY,{"derivedFrom":makeQuery(id+"F4.opPattern","COPY",BODY,{"derivedFrom":makeQuery(id+"F2.opPattern","COPY",BODY,{"derivedFrom":makeQuery(id+"F1.opRevolve","SWEPT_BODY",BODY,{"disambiguationData":[OSD([sQuery(id+"F0.wireOp",EDGE,"E1")])]}),"instanceName":"1"}),"instanceName":"1"}),"instanceName":"1"}),"instanceName":"1"}),"instanceName":"1"}),"instanceName":"1"});
            var Q982;
            Q982=makeQuery(id+"F12.opPattern","COPY",BODY,{"derivedFrom":makeQuery(id+"F10.opPattern","COPY",BODY,{"derivedFrom":makeQuery(id+"F6.opPattern","COPY",BODY,{"derivedFrom":makeQuery(id+"F5.opPattern","COPY",BODY,{"derivedFrom":makeQuery(id+"F4.opPattern","COPY",BODY,{"derivedFrom":makeQuery(id+"F3.opPattern","COPY",BODY,{"derivedFrom":makeQuery(id+"F2.opPattern","COPY",BODY,{"derivedFrom":makeQuery(id+"F1.opRevolve","SWEPT_BODY",BODY,{"disambiguationData":[OSD([sQuery(id+"F0.wireOp",EDGE,"E1")])]}),"instanceName":"1"}),"instanceName":"1"}),"instanceName":"1"}),"instanceName":"1"}),"instanceName":"1"}),"instanceName":"1"}),"instanceName":"1"});
            var Q983;
            Q983=makeQuery(id+"F12.opPattern","COPY",BODY,{"derivedFrom":makeQuery(id+"F10.opPattern","COPY",BODY,{"derivedFrom":makeQuery(id+"F7.opPattern","COPY",BODY,{"derivedFrom":makeQuery(id+"F1.opRevolve","SWEPT_BODY",BODY,{"disambiguationData":[OSD([sQuery(id+"F0.wireOp",EDGE,"E1")])]}),"instanceName":"1"}),"instanceName":"1"}),"instanceName":"1"});
            var Q984;
            Q984=makeQuery(id+"F12.opPattern","COPY",BODY,{"derivedFrom":makeQuery(id+"F10.opPattern","COPY",BODY,{"derivedFrom":makeQuery(id+"F7.opPattern","COPY",BODY,{"derivedFrom":makeQuery(id+"F2.opPattern","COPY",BODY,{"derivedFrom":makeQuery(id+"F1.opRevolve","SWEPT_BODY",BODY,{"disambiguationData":[OSD([sQuery(id+"F0.wireOp",EDGE,"E1")])]}),"instanceName":"1"}),"instanceName":"1"}),"instanceName":"1"}),"instanceName":"1"});
            var Q985;
            Q985=makeQuery(id+"F12.opPattern","COPY",BODY,{"derivedFrom":makeQuery(id+"F10.opPattern","COPY",BODY,{"derivedFrom":makeQuery(id+"F7.opPattern","COPY",BODY,{"derivedFrom":makeQuery(id+"F3.opPattern","COPY",BODY,{"derivedFrom":makeQuery(id+"F2.opPattern","COPY",BODY,{"derivedFrom":makeQuery(id+"F1.opRevolve","SWEPT_BODY",BODY,{"disambiguationData":[OSD([sQuery(id+"F0.wireOp",EDGE,"E1")])]}),"instanceName":"1"}),"instanceName":"1"}),"instanceName":"1"}),"instanceName":"1"}),"instanceName":"1"});
            var Q986;
            Q986=makeQuery(id+"F12.opPattern","COPY",BODY,{"derivedFrom":makeQuery(id+"F10.opPattern","COPY",BODY,{"derivedFrom":makeQuery(id+"F7.opPattern","COPY",BODY,{"derivedFrom":makeQuery(id+"F4.opPattern","COPY",BODY,{"derivedFrom":makeQuery(id+"F1.opRevolve","SWEPT_BODY",BODY,{"disambiguationData":[OSD([sQuery(id+"F0.wireOp",EDGE,"E1")])]}),"instanceName":"1"}),"instanceName":"1"}),"instanceName":"1"}),"instanceName":"1"});
            var Q987;
            Q987=makeQuery(id+"F12.opPattern","COPY",BODY,{"derivedFrom":makeQuery(id+"F10.opPattern","COPY",BODY,{"derivedFrom":makeQuery(id+"F7.opPattern","COPY",BODY,{"derivedFrom":makeQuery(id+"F4.opPattern","COPY",BODY,{"derivedFrom":makeQuery(id+"F2.opPattern","COPY",BODY,{"derivedFrom":makeQuery(id+"F1.opRevolve","SWEPT_BODY",BODY,{"disambiguationData":[OSD([sQuery(id+"F0.wireOp",EDGE,"E1")])]}),"instanceName":"1"}),"instanceName":"1"}),"instanceName":"1"}),"instanceName":"1"}),"instanceName":"1"});
            var Q988;
            Q988=makeQuery(id+"F12.opPattern","COPY",BODY,{"derivedFrom":makeQuery(id+"F10.opPattern","COPY",BODY,{"derivedFrom":makeQuery(id+"F7.opPattern","COPY",BODY,{"derivedFrom":makeQuery(id+"F4.opPattern","COPY",BODY,{"derivedFrom":makeQuery(id+"F3.opPattern","COPY",BODY,{"derivedFrom":makeQuery(id+"F2.opPattern","COPY",BODY,{"derivedFrom":makeQuery(id+"F1.opRevolve","SWEPT_BODY",BODY,{"disambiguationData":[OSD([sQuery(id+"F0.wireOp",EDGE,"E1")])]}),"instanceName":"1"}),"instanceName":"1"}),"instanceName":"1"}),"instanceName":"1"}),"instanceName":"1"}),"instanceName":"1"});
            var Q989;
            Q989=makeQuery(id+"F12.opPattern","COPY",BODY,{"derivedFrom":makeQuery(id+"F10.opPattern","COPY",BODY,{"derivedFrom":makeQuery(id+"F7.opPattern","COPY",BODY,{"derivedFrom":makeQuery(id+"F5.opPattern","COPY",BODY,{"derivedFrom":makeQuery(id+"F1.opRevolve","SWEPT_BODY",BODY,{"disambiguationData":[OSD([sQuery(id+"F0.wireOp",EDGE,"E1")])]}),"instanceName":"1"}),"instanceName":"1"}),"instanceName":"1"}),"instanceName":"1"});
            var Q990;
            Q990=makeQuery(id+"F12.opPattern","COPY",BODY,{"derivedFrom":makeQuery(id+"F10.opPattern","COPY",BODY,{"derivedFrom":makeQuery(id+"F7.opPattern","COPY",BODY,{"derivedFrom":makeQuery(id+"F5.opPattern","COPY",BODY,{"derivedFrom":makeQuery(id+"F2.opPattern","COPY",BODY,{"derivedFrom":makeQuery(id+"F1.opRevolve","SWEPT_BODY",BODY,{"disambiguationData":[OSD([sQuery(id+"F0.wireOp",EDGE,"E1")])]}),"instanceName":"1"}),"instanceName":"1"}),"instanceName":"1"}),"instanceName":"1"}),"instanceName":"1"});
            var Q991;
            Q991=makeQuery(id+"F12.opPattern","COPY",BODY,{"derivedFrom":makeQuery(id+"F10.opPattern","COPY",BODY,{"derivedFrom":makeQuery(id+"F7.opPattern","COPY",BODY,{"derivedFrom":makeQuery(id+"F5.opPattern","COPY",BODY,{"derivedFrom":makeQuery(id+"F3.opPattern","COPY",BODY,{"derivedFrom":makeQuery(id+"F2.opPattern","COPY",BODY,{"derivedFrom":makeQuery(id+"F1.opRevolve","SWEPT_BODY",BODY,{"disambiguationData":[OSD([sQuery(id+"F0.wireOp",EDGE,"E1")])]}),"instanceName":"1"}),"instanceName":"1"}),"instanceName":"1"}),"instanceName":"1"}),"instanceName":"1"}),"instanceName":"1"});
            var Q992;
            Q992=makeQuery(id+"F12.opPattern","COPY",BODY,{"derivedFrom":makeQuery(id+"F10.opPattern","COPY",BODY,{"derivedFrom":makeQuery(id+"F7.opPattern","COPY",BODY,{"derivedFrom":makeQuery(id+"F5.opPattern","COPY",BODY,{"derivedFrom":makeQuery(id+"F4.opPattern","COPY",BODY,{"derivedFrom":makeQuery(id+"F1.opRevolve","SWEPT_BODY",BODY,{"disambiguationData":[OSD([sQuery(id+"F0.wireOp",EDGE,"E1")])]}),"instanceName":"1"}),"instanceName":"1"}),"instanceName":"1"}),"instanceName":"1"}),"instanceName":"1"});
            var Q993;
            Q993=makeQuery(id+"F12.opPattern","COPY",BODY,{"derivedFrom":makeQuery(id+"F10.opPattern","COPY",BODY,{"derivedFrom":makeQuery(id+"F7.opPattern","COPY",BODY,{"derivedFrom":makeQuery(id+"F5.opPattern","COPY",BODY,{"derivedFrom":makeQuery(id+"F4.opPattern","COPY",BODY,{"derivedFrom":makeQuery(id+"F2.opPattern","COPY",BODY,{"derivedFrom":makeQuery(id+"F1.opRevolve","SWEPT_BODY",BODY,{"disambiguationData":[OSD([sQuery(id+"F0.wireOp",EDGE,"E1")])]}),"instanceName":"1"}),"instanceName":"1"}),"instanceName":"1"}),"instanceName":"1"}),"instanceName":"1"}),"instanceName":"1"});
            var Q994;
            Q994=makeQuery(id+"F12.opPattern","COPY",BODY,{"derivedFrom":makeQuery(id+"F10.opPattern","COPY",BODY,{"derivedFrom":makeQuery(id+"F7.opPattern","COPY",BODY,{"derivedFrom":makeQuery(id+"F5.opPattern","COPY",BODY,{"derivedFrom":makeQuery(id+"F4.opPattern","COPY",BODY,{"derivedFrom":makeQuery(id+"F3.opPattern","COPY",BODY,{"derivedFrom":makeQuery(id+"F2.opPattern","COPY",BODY,{"derivedFrom":makeQuery(id+"F1.opRevolve","SWEPT_BODY",BODY,{"disambiguationData":[OSD([sQuery(id+"F0.wireOp",EDGE,"E1")])]}),"instanceName":"1"}),"instanceName":"1"}),"instanceName":"1"}),"instanceName":"1"}),"instanceName":"1"}),"instanceName":"1"}),"instanceName":"1"});
            var Q995;
            Q995=makeQuery(id+"F12.opPattern","COPY",BODY,{"derivedFrom":makeQuery(id+"F10.opPattern","COPY",BODY,{"derivedFrom":makeQuery(id+"F7.opPattern","COPY",BODY,{"derivedFrom":makeQuery(id+"F6.opPattern","COPY",BODY,{"derivedFrom":makeQuery(id+"F1.opRevolve","SWEPT_BODY",BODY,{"disambiguationData":[OSD([sQuery(id+"F0.wireOp",EDGE,"E1")])]}),"instanceName":"1"}),"instanceName":"1"}),"instanceName":"1"}),"instanceName":"1"});
            var Q996;
            Q996=makeQuery(id+"F12.opPattern","COPY",BODY,{"derivedFrom":makeQuery(id+"F10.opPattern","COPY",BODY,{"derivedFrom":makeQuery(id+"F7.opPattern","COPY",BODY,{"derivedFrom":makeQuery(id+"F6.opPattern","COPY",BODY,{"derivedFrom":makeQuery(id+"F2.opPattern","COPY",BODY,{"derivedFrom":makeQuery(id+"F1.opRevolve","SWEPT_BODY",BODY,{"disambiguationData":[OSD([sQuery(id+"F0.wireOp",EDGE,"E1")])]}),"instanceName":"1"}),"instanceName":"1"}),"instanceName":"1"}),"instanceName":"1"}),"instanceName":"1"});
            var Q997;
            Q997=makeQuery(id+"F12.opPattern","COPY",BODY,{"derivedFrom":makeQuery(id+"F10.opPattern","COPY",BODY,{"derivedFrom":makeQuery(id+"F7.opPattern","COPY",BODY,{"derivedFrom":makeQuery(id+"F6.opPattern","COPY",BODY,{"derivedFrom":makeQuery(id+"F3.opPattern","COPY",BODY,{"derivedFrom":makeQuery(id+"F2.opPattern","COPY",BODY,{"derivedFrom":makeQuery(id+"F1.opRevolve","SWEPT_BODY",BODY,{"disambiguationData":[OSD([sQuery(id+"F0.wireOp",EDGE,"E1")])]}),"instanceName":"1"}),"instanceName":"1"}),"instanceName":"1"}),"instanceName":"1"}),"instanceName":"1"}),"instanceName":"1"});
            var Q998;
            Q998=makeQuery(id+"F12.opPattern","COPY",BODY,{"derivedFrom":makeQuery(id+"F10.opPattern","COPY",BODY,{"derivedFrom":makeQuery(id+"F7.opPattern","COPY",BODY,{"derivedFrom":makeQuery(id+"F6.opPattern","COPY",BODY,{"derivedFrom":makeQuery(id+"F4.opPattern","COPY",BODY,{"derivedFrom":makeQuery(id+"F1.opRevolve","SWEPT_BODY",BODY,{"disambiguationData":[OSD([sQuery(id+"F0.wireOp",EDGE,"E1")])]}),"instanceName":"1"}),"instanceName":"1"}),"instanceName":"1"}),"instanceName":"1"}),"instanceName":"1"});
            var Q999;
            Q999=makeQuery(id+"F12.opPattern","COPY",BODY,{"derivedFrom":makeQuery(id+"F10.opPattern","COPY",BODY,{"derivedFrom":makeQuery(id+"F7.opPattern","COPY",BODY,{"derivedFrom":makeQuery(id+"F6.opPattern","COPY",BODY,{"derivedFrom":makeQuery(id+"F4.opPattern","COPY",BODY,{"derivedFrom":makeQuery(id+"F2.opPattern","COPY",BODY,{"derivedFrom":makeQuery(id+"F1.opRevolve","SWEPT_BODY",BODY,{"disambiguationData":[OSD([sQuery(id+"F0.wireOp",EDGE,"E1")])]}),"instanceName":"1"}),"instanceName":"1"}),"instanceName":"1"}),"instanceName":"1"}),"instanceName":"1"}),"instanceName":"1"});
            var Q1000;
            Q1000=makeQuery(id+"F12.opPattern","COPY",BODY,{"derivedFrom":makeQuery(id+"F10.opPattern","COPY",BODY,{"derivedFrom":makeQuery(id+"F7.opPattern","COPY",BODY,{"derivedFrom":makeQuery(id+"F6.opPattern","COPY",BODY,{"derivedFrom":makeQuery(id+"F4.opPattern","COPY",BODY,{"derivedFrom":makeQuery(id+"F3.opPattern","COPY",BODY,{"derivedFrom":makeQuery(id+"F2.opPattern","COPY",BODY,{"derivedFrom":makeQuery(id+"F1.opRevolve","SWEPT_BODY",BODY,{"disambiguationData":[OSD([sQuery(id+"F0.wireOp",EDGE,"E1")])]}),"instanceName":"1"}),"instanceName":"1"}),"instanceName":"1"}),"instanceName":"1"}),"instanceName":"1"}),"instanceName":"1"}),"instanceName":"1"});
            var Q1001;
            Q1001=makeQuery(id+"F12.opPattern","COPY",BODY,{"derivedFrom":makeQuery(id+"F10.opPattern","COPY",BODY,{"derivedFrom":makeQuery(id+"F7.opPattern","COPY",BODY,{"derivedFrom":makeQuery(id+"F6.opPattern","COPY",BODY,{"derivedFrom":makeQuery(id+"F5.opPattern","COPY",BODY,{"derivedFrom":makeQuery(id+"F1.opRevolve","SWEPT_BODY",BODY,{"disambiguationData":[OSD([sQuery(id+"F0.wireOp",EDGE,"E1")])]}),"instanceName":"1"}),"instanceName":"1"}),"instanceName":"1"}),"instanceName":"1"}),"instanceName":"1"});
            var Q1002;
            Q1002=makeQuery(id+"F12.opPattern","COPY",BODY,{"derivedFrom":makeQuery(id+"F10.opPattern","COPY",BODY,{"derivedFrom":makeQuery(id+"F7.opPattern","COPY",BODY,{"derivedFrom":makeQuery(id+"F6.opPattern","COPY",BODY,{"derivedFrom":makeQuery(id+"F5.opPattern","COPY",BODY,{"derivedFrom":makeQuery(id+"F2.opPattern","COPY",BODY,{"derivedFrom":makeQuery(id+"F1.opRevolve","SWEPT_BODY",BODY,{"disambiguationData":[OSD([sQuery(id+"F0.wireOp",EDGE,"E1")])]}),"instanceName":"1"}),"instanceName":"1"}),"instanceName":"1"}),"instanceName":"1"}),"instanceName":"1"}),"instanceName":"1"});
            var Q1003;
            Q1003=makeQuery(id+"F12.opPattern","COPY",BODY,{"derivedFrom":makeQuery(id+"F10.opPattern","COPY",BODY,{"derivedFrom":makeQuery(id+"F7.opPattern","COPY",BODY,{"derivedFrom":makeQuery(id+"F6.opPattern","COPY",BODY,{"derivedFrom":makeQuery(id+"F5.opPattern","COPY",BODY,{"derivedFrom":makeQuery(id+"F3.opPattern","COPY",BODY,{"derivedFrom":makeQuery(id+"F2.opPattern","COPY",BODY,{"derivedFrom":makeQuery(id+"F1.opRevolve","SWEPT_BODY",BODY,{"disambiguationData":[OSD([sQuery(id+"F0.wireOp",EDGE,"E1")])]}),"instanceName":"1"}),"instanceName":"1"}),"instanceName":"1"}),"instanceName":"1"}),"instanceName":"1"}),"instanceName":"1"}),"instanceName":"1"});
            var Q1004;
            Q1004=makeQuery(id+"F12.opPattern","COPY",BODY,{"derivedFrom":makeQuery(id+"F10.opPattern","COPY",BODY,{"derivedFrom":makeQuery(id+"F7.opPattern","COPY",BODY,{"derivedFrom":makeQuery(id+"F6.opPattern","COPY",BODY,{"derivedFrom":makeQuery(id+"F5.opPattern","COPY",BODY,{"derivedFrom":makeQuery(id+"F4.opPattern","COPY",BODY,{"derivedFrom":makeQuery(id+"F1.opRevolve","SWEPT_BODY",BODY,{"disambiguationData":[OSD([sQuery(id+"F0.wireOp",EDGE,"E1")])]}),"instanceName":"1"}),"instanceName":"1"}),"instanceName":"1"}),"instanceName":"1"}),"instanceName":"1"}),"instanceName":"1"});
            var Q1005;
            Q1005=makeQuery(id+"F12.opPattern","COPY",BODY,{"derivedFrom":makeQuery(id+"F10.opPattern","COPY",BODY,{"derivedFrom":makeQuery(id+"F7.opPattern","COPY",BODY,{"derivedFrom":makeQuery(id+"F6.opPattern","COPY",BODY,{"derivedFrom":makeQuery(id+"F5.opPattern","COPY",BODY,{"derivedFrom":makeQuery(id+"F4.opPattern","COPY",BODY,{"derivedFrom":makeQuery(id+"F2.opPattern","COPY",BODY,{"derivedFrom":makeQuery(id+"F1.opRevolve","SWEPT_BODY",BODY,{"disambiguationData":[OSD([sQuery(id+"F0.wireOp",EDGE,"E1")])]}),"instanceName":"1"}),"instanceName":"1"}),"instanceName":"1"}),"instanceName":"1"}),"instanceName":"1"}),"instanceName":"1"}),"instanceName":"1"});
            var Q1006;
            Q1006=makeQuery(id+"F12.opPattern","COPY",BODY,{"derivedFrom":makeQuery(id+"F10.opPattern","COPY",BODY,{"derivedFrom":makeQuery(id+"F7.opPattern","COPY",BODY,{"derivedFrom":makeQuery(id+"F6.opPattern","COPY",BODY,{"derivedFrom":makeQuery(id+"F5.opPattern","COPY",BODY,{"derivedFrom":makeQuery(id+"F4.opPattern","COPY",BODY,{"derivedFrom":makeQuery(id+"F3.opPattern","COPY",BODY,{"derivedFrom":makeQuery(id+"F2.opPattern","COPY",BODY,{"derivedFrom":makeQuery(id+"F1.opRevolve","SWEPT_BODY",BODY,{"disambiguationData":[OSD([sQuery(id+"F0.wireOp",EDGE,"E1")])]}),"instanceName":"1"}),"instanceName":"1"}),"instanceName":"1"}),"instanceName":"1"}),"instanceName":"1"}),"instanceName":"1"}),"instanceName":"1"}),"instanceName":"1"});
            var Q1007;
            Q1007=makeQuery(id+"F12.opPattern","COPY",BODY,{"derivedFrom":makeQuery(id+"F10.opPattern","COPY",BODY,{"derivedFrom":makeQuery(id+"F8.opPattern","COPY",BODY,{"derivedFrom":makeQuery(id+"F1.opRevolve","SWEPT_BODY",BODY,{"disambiguationData":[OSD([sQuery(id+"F0.wireOp",EDGE,"E1")])]}),"instanceName":"1"}),"instanceName":"1"}),"instanceName":"1"});
            var Q1008;
            Q1008=makeQuery(id+"F12.opPattern","COPY",BODY,{"derivedFrom":makeQuery(id+"F10.opPattern","COPY",BODY,{"derivedFrom":makeQuery(id+"F8.opPattern","COPY",BODY,{"derivedFrom":makeQuery(id+"F2.opPattern","COPY",BODY,{"derivedFrom":makeQuery(id+"F1.opRevolve","SWEPT_BODY",BODY,{"disambiguationData":[OSD([sQuery(id+"F0.wireOp",EDGE,"E1")])]}),"instanceName":"1"}),"instanceName":"1"}),"instanceName":"1"}),"instanceName":"1"});
            var Q1009;
            Q1009=makeQuery(id+"F12.opPattern","COPY",BODY,{"derivedFrom":makeQuery(id+"F10.opPattern","COPY",BODY,{"derivedFrom":makeQuery(id+"F8.opPattern","COPY",BODY,{"derivedFrom":makeQuery(id+"F3.opPattern","COPY",BODY,{"derivedFrom":makeQuery(id+"F2.opPattern","COPY",BODY,{"derivedFrom":makeQuery(id+"F1.opRevolve","SWEPT_BODY",BODY,{"disambiguationData":[OSD([sQuery(id+"F0.wireOp",EDGE,"E1")])]}),"instanceName":"1"}),"instanceName":"1"}),"instanceName":"1"}),"instanceName":"1"}),"instanceName":"1"});
            var Q1010;
            Q1010=makeQuery(id+"F12.opPattern","COPY",BODY,{"derivedFrom":makeQuery(id+"F10.opPattern","COPY",BODY,{"derivedFrom":makeQuery(id+"F8.opPattern","COPY",BODY,{"derivedFrom":makeQuery(id+"F4.opPattern","COPY",BODY,{"derivedFrom":makeQuery(id+"F1.opRevolve","SWEPT_BODY",BODY,{"disambiguationData":[OSD([sQuery(id+"F0.wireOp",EDGE,"E1")])]}),"instanceName":"1"}),"instanceName":"1"}),"instanceName":"1"}),"instanceName":"1"});
            var Q1011;
            Q1011=makeQuery(id+"F12.opPattern","COPY",BODY,{"derivedFrom":makeQuery(id+"F10.opPattern","COPY",BODY,{"derivedFrom":makeQuery(id+"F8.opPattern","COPY",BODY,{"derivedFrom":makeQuery(id+"F4.opPattern","COPY",BODY,{"derivedFrom":makeQuery(id+"F2.opPattern","COPY",BODY,{"derivedFrom":makeQuery(id+"F1.opRevolve","SWEPT_BODY",BODY,{"disambiguationData":[OSD([sQuery(id+"F0.wireOp",EDGE,"E1")])]}),"instanceName":"1"}),"instanceName":"1"}),"instanceName":"1"}),"instanceName":"1"}),"instanceName":"1"});
            var Q1012;
            Q1012=makeQuery(id+"F12.opPattern","COPY",BODY,{"derivedFrom":makeQuery(id+"F10.opPattern","COPY",BODY,{"derivedFrom":makeQuery(id+"F8.opPattern","COPY",BODY,{"derivedFrom":makeQuery(id+"F4.opPattern","COPY",BODY,{"derivedFrom":makeQuery(id+"F3.opPattern","COPY",BODY,{"derivedFrom":makeQuery(id+"F2.opPattern","COPY",BODY,{"derivedFrom":makeQuery(id+"F1.opRevolve","SWEPT_BODY",BODY,{"disambiguationData":[OSD([sQuery(id+"F0.wireOp",EDGE,"E1")])]}),"instanceName":"1"}),"instanceName":"1"}),"instanceName":"1"}),"instanceName":"1"}),"instanceName":"1"}),"instanceName":"1"});
            var Q1013;
            Q1013=makeQuery(id+"F12.opPattern","COPY",BODY,{"derivedFrom":makeQuery(id+"F10.opPattern","COPY",BODY,{"derivedFrom":makeQuery(id+"F8.opPattern","COPY",BODY,{"derivedFrom":makeQuery(id+"F5.opPattern","COPY",BODY,{"derivedFrom":makeQuery(id+"F1.opRevolve","SWEPT_BODY",BODY,{"disambiguationData":[OSD([sQuery(id+"F0.wireOp",EDGE,"E1")])]}),"instanceName":"1"}),"instanceName":"1"}),"instanceName":"1"}),"instanceName":"1"});
            var Q1014;
            Q1014=makeQuery(id+"F12.opPattern","COPY",BODY,{"derivedFrom":makeQuery(id+"F10.opPattern","COPY",BODY,{"derivedFrom":makeQuery(id+"F8.opPattern","COPY",BODY,{"derivedFrom":makeQuery(id+"F5.opPattern","COPY",BODY,{"derivedFrom":makeQuery(id+"F2.opPattern","COPY",BODY,{"derivedFrom":makeQuery(id+"F1.opRevolve","SWEPT_BODY",BODY,{"disambiguationData":[OSD([sQuery(id+"F0.wireOp",EDGE,"E1")])]}),"instanceName":"1"}),"instanceName":"1"}),"instanceName":"1"}),"instanceName":"1"}),"instanceName":"1"});
            var Q1015;
            Q1015=makeQuery(id+"F12.opPattern","COPY",BODY,{"derivedFrom":makeQuery(id+"F10.opPattern","COPY",BODY,{"derivedFrom":makeQuery(id+"F8.opPattern","COPY",BODY,{"derivedFrom":makeQuery(id+"F5.opPattern","COPY",BODY,{"derivedFrom":makeQuery(id+"F3.opPattern","COPY",BODY,{"derivedFrom":makeQuery(id+"F2.opPattern","COPY",BODY,{"derivedFrom":makeQuery(id+"F1.opRevolve","SWEPT_BODY",BODY,{"disambiguationData":[OSD([sQuery(id+"F0.wireOp",EDGE,"E1")])]}),"instanceName":"1"}),"instanceName":"1"}),"instanceName":"1"}),"instanceName":"1"}),"instanceName":"1"}),"instanceName":"1"});
            var Q1016;
            Q1016=makeQuery(id+"F12.opPattern","COPY",BODY,{"derivedFrom":makeQuery(id+"F10.opPattern","COPY",BODY,{"derivedFrom":makeQuery(id+"F8.opPattern","COPY",BODY,{"derivedFrom":makeQuery(id+"F5.opPattern","COPY",BODY,{"derivedFrom":makeQuery(id+"F4.opPattern","COPY",BODY,{"derivedFrom":makeQuery(id+"F1.opRevolve","SWEPT_BODY",BODY,{"disambiguationData":[OSD([sQuery(id+"F0.wireOp",EDGE,"E1")])]}),"instanceName":"1"}),"instanceName":"1"}),"instanceName":"1"}),"instanceName":"1"}),"instanceName":"1"});
            var Q1017;
            Q1017=makeQuery(id+"F12.opPattern","COPY",BODY,{"derivedFrom":makeQuery(id+"F10.opPattern","COPY",BODY,{"derivedFrom":makeQuery(id+"F8.opPattern","COPY",BODY,{"derivedFrom":makeQuery(id+"F5.opPattern","COPY",BODY,{"derivedFrom":makeQuery(id+"F4.opPattern","COPY",BODY,{"derivedFrom":makeQuery(id+"F2.opPattern","COPY",BODY,{"derivedFrom":makeQuery(id+"F1.opRevolve","SWEPT_BODY",BODY,{"disambiguationData":[OSD([sQuery(id+"F0.wireOp",EDGE,"E1")])]}),"instanceName":"1"}),"instanceName":"1"}),"instanceName":"1"}),"instanceName":"1"}),"instanceName":"1"}),"instanceName":"1"});
            var Q1018;
            Q1018=makeQuery(id+"F12.opPattern","COPY",BODY,{"derivedFrom":makeQuery(id+"F10.opPattern","COPY",BODY,{"derivedFrom":makeQuery(id+"F8.opPattern","COPY",BODY,{"derivedFrom":makeQuery(id+"F5.opPattern","COPY",BODY,{"derivedFrom":makeQuery(id+"F4.opPattern","COPY",BODY,{"derivedFrom":makeQuery(id+"F3.opPattern","COPY",BODY,{"derivedFrom":makeQuery(id+"F2.opPattern","COPY",BODY,{"derivedFrom":makeQuery(id+"F1.opRevolve","SWEPT_BODY",BODY,{"disambiguationData":[OSD([sQuery(id+"F0.wireOp",EDGE,"E1")])]}),"instanceName":"1"}),"instanceName":"1"}),"instanceName":"1"}),"instanceName":"1"}),"instanceName":"1"}),"instanceName":"1"}),"instanceName":"1"});
            var Q1019;
            Q1019=makeQuery(id+"F12.opPattern","COPY",BODY,{"derivedFrom":makeQuery(id+"F10.opPattern","COPY",BODY,{"derivedFrom":makeQuery(id+"F8.opPattern","COPY",BODY,{"derivedFrom":makeQuery(id+"F6.opPattern","COPY",BODY,{"derivedFrom":makeQuery(id+"F1.opRevolve","SWEPT_BODY",BODY,{"disambiguationData":[OSD([sQuery(id+"F0.wireOp",EDGE,"E1")])]}),"instanceName":"1"}),"instanceName":"1"}),"instanceName":"1"}),"instanceName":"1"});
            var Q1020;
            Q1020=makeQuery(id+"F12.opPattern","COPY",BODY,{"derivedFrom":makeQuery(id+"F10.opPattern","COPY",BODY,{"derivedFrom":makeQuery(id+"F8.opPattern","COPY",BODY,{"derivedFrom":makeQuery(id+"F6.opPattern","COPY",BODY,{"derivedFrom":makeQuery(id+"F2.opPattern","COPY",BODY,{"derivedFrom":makeQuery(id+"F1.opRevolve","SWEPT_BODY",BODY,{"disambiguationData":[OSD([sQuery(id+"F0.wireOp",EDGE,"E1")])]}),"instanceName":"1"}),"instanceName":"1"}),"instanceName":"1"}),"instanceName":"1"}),"instanceName":"1"});
            var Q1021;
            Q1021=makeQuery(id+"F12.opPattern","COPY",BODY,{"derivedFrom":makeQuery(id+"F10.opPattern","COPY",BODY,{"derivedFrom":makeQuery(id+"F8.opPattern","COPY",BODY,{"derivedFrom":makeQuery(id+"F6.opPattern","COPY",BODY,{"derivedFrom":makeQuery(id+"F3.opPattern","COPY",BODY,{"derivedFrom":makeQuery(id+"F2.opPattern","COPY",BODY,{"derivedFrom":makeQuery(id+"F1.opRevolve","SWEPT_BODY",BODY,{"disambiguationData":[OSD([sQuery(id+"F0.wireOp",EDGE,"E1")])]}),"instanceName":"1"}),"instanceName":"1"}),"instanceName":"1"}),"instanceName":"1"}),"instanceName":"1"}),"instanceName":"1"});
            var Q1022;
            Q1022=makeQuery(id+"F12.opPattern","COPY",BODY,{"derivedFrom":makeQuery(id+"F10.opPattern","COPY",BODY,{"derivedFrom":makeQuery(id+"F8.opPattern","COPY",BODY,{"derivedFrom":makeQuery(id+"F6.opPattern","COPY",BODY,{"derivedFrom":makeQuery(id+"F4.opPattern","COPY",BODY,{"derivedFrom":makeQuery(id+"F1.opRevolve","SWEPT_BODY",BODY,{"disambiguationData":[OSD([sQuery(id+"F0.wireOp",EDGE,"E1")])]}),"instanceName":"1"}),"instanceName":"1"}),"instanceName":"1"}),"instanceName":"1"}),"instanceName":"1"});
            var Q1023;
            Q1023=makeQuery(id+"F12.opPattern","COPY",BODY,{"derivedFrom":makeQuery(id+"F10.opPattern","COPY",BODY,{"derivedFrom":makeQuery(id+"F8.opPattern","COPY",BODY,{"derivedFrom":makeQuery(id+"F6.opPattern","COPY",BODY,{"derivedFrom":makeQuery(id+"F4.opPattern","COPY",BODY,{"derivedFrom":makeQuery(id+"F2.opPattern","COPY",BODY,{"derivedFrom":makeQuery(id+"F1.opRevolve","SWEPT_BODY",BODY,{"disambiguationData":[OSD([sQuery(id+"F0.wireOp",EDGE,"E1")])]}),"instanceName":"1"}),"instanceName":"1"}),"instanceName":"1"}),"instanceName":"1"}),"instanceName":"1"}),"instanceName":"1"});
            var Q1024;
            Q1024=makeQuery(id+"F12.opPattern","COPY",BODY,{"derivedFrom":makeQuery(id+"F10.opPattern","COPY",BODY,{"derivedFrom":makeQuery(id+"F8.opPattern","COPY",BODY,{"derivedFrom":makeQuery(id+"F6.opPattern","COPY",BODY,{"derivedFrom":makeQuery(id+"F4.opPattern","COPY",BODY,{"derivedFrom":makeQuery(id+"F3.opPattern","COPY",BODY,{"derivedFrom":makeQuery(id+"F2.opPattern","COPY",BODY,{"derivedFrom":makeQuery(id+"F1.opRevolve","SWEPT_BODY",BODY,{"disambiguationData":[OSD([sQuery(id+"F0.wireOp",EDGE,"E1")])]}),"instanceName":"1"}),"instanceName":"1"}),"instanceName":"1"}),"instanceName":"1"}),"instanceName":"1"}),"instanceName":"1"}),"instanceName":"1"});
            var Q1025;
            Q1025=makeQuery(id+"F12.opPattern","COPY",BODY,{"derivedFrom":makeQuery(id+"F10.opPattern","COPY",BODY,{"derivedFrom":makeQuery(id+"F8.opPattern","COPY",BODY,{"derivedFrom":makeQuery(id+"F6.opPattern","COPY",BODY,{"derivedFrom":makeQuery(id+"F5.opPattern","COPY",BODY,{"derivedFrom":makeQuery(id+"F1.opRevolve","SWEPT_BODY",BODY,{"disambiguationData":[OSD([sQuery(id+"F0.wireOp",EDGE,"E1")])]}),"instanceName":"1"}),"instanceName":"1"}),"instanceName":"1"}),"instanceName":"1"}),"instanceName":"1"});
            var Q1026;
            Q1026=makeQuery(id+"F12.opPattern","COPY",BODY,{"derivedFrom":makeQuery(id+"F10.opPattern","COPY",BODY,{"derivedFrom":makeQuery(id+"F8.opPattern","COPY",BODY,{"derivedFrom":makeQuery(id+"F6.opPattern","COPY",BODY,{"derivedFrom":makeQuery(id+"F5.opPattern","COPY",BODY,{"derivedFrom":makeQuery(id+"F2.opPattern","COPY",BODY,{"derivedFrom":makeQuery(id+"F1.opRevolve","SWEPT_BODY",BODY,{"disambiguationData":[OSD([sQuery(id+"F0.wireOp",EDGE,"E1")])]}),"instanceName":"1"}),"instanceName":"1"}),"instanceName":"1"}),"instanceName":"1"}),"instanceName":"1"}),"instanceName":"1"});
            var Q1027;
            Q1027=makeQuery(id+"F12.opPattern","COPY",BODY,{"derivedFrom":makeQuery(id+"F10.opPattern","COPY",BODY,{"derivedFrom":makeQuery(id+"F8.opPattern","COPY",BODY,{"derivedFrom":makeQuery(id+"F6.opPattern","COPY",BODY,{"derivedFrom":makeQuery(id+"F5.opPattern","COPY",BODY,{"derivedFrom":makeQuery(id+"F3.opPattern","COPY",BODY,{"derivedFrom":makeQuery(id+"F2.opPattern","COPY",BODY,{"derivedFrom":makeQuery(id+"F1.opRevolve","SWEPT_BODY",BODY,{"disambiguationData":[OSD([sQuery(id+"F0.wireOp",EDGE,"E1")])]}),"instanceName":"1"}),"instanceName":"1"}),"instanceName":"1"}),"instanceName":"1"}),"instanceName":"1"}),"instanceName":"1"}),"instanceName":"1"});
            var Q1028;
            Q1028=makeQuery(id+"F12.opPattern","COPY",BODY,{"derivedFrom":makeQuery(id+"F10.opPattern","COPY",BODY,{"derivedFrom":makeQuery(id+"F8.opPattern","COPY",BODY,{"derivedFrom":makeQuery(id+"F6.opPattern","COPY",BODY,{"derivedFrom":makeQuery(id+"F5.opPattern","COPY",BODY,{"derivedFrom":makeQuery(id+"F4.opPattern","COPY",BODY,{"derivedFrom":makeQuery(id+"F1.opRevolve","SWEPT_BODY",BODY,{"disambiguationData":[OSD([sQuery(id+"F0.wireOp",EDGE,"E1")])]}),"instanceName":"1"}),"instanceName":"1"}),"instanceName":"1"}),"instanceName":"1"}),"instanceName":"1"}),"instanceName":"1"});
            var Q1029;
            Q1029=makeQuery(id+"F12.opPattern","COPY",BODY,{"derivedFrom":makeQuery(id+"F10.opPattern","COPY",BODY,{"derivedFrom":makeQuery(id+"F8.opPattern","COPY",BODY,{"derivedFrom":makeQuery(id+"F6.opPattern","COPY",BODY,{"derivedFrom":makeQuery(id+"F5.opPattern","COPY",BODY,{"derivedFrom":makeQuery(id+"F4.opPattern","COPY",BODY,{"derivedFrom":makeQuery(id+"F2.opPattern","COPY",BODY,{"derivedFrom":makeQuery(id+"F1.opRevolve","SWEPT_BODY",BODY,{"disambiguationData":[OSD([sQuery(id+"F0.wireOp",EDGE,"E1")])]}),"instanceName":"1"}),"instanceName":"1"}),"instanceName":"1"}),"instanceName":"1"}),"instanceName":"1"}),"instanceName":"1"}),"instanceName":"1"});
            var Q1030;
            Q1030=makeQuery(id+"F12.opPattern","COPY",BODY,{"derivedFrom":makeQuery(id+"F10.opPattern","COPY",BODY,{"derivedFrom":makeQuery(id+"F8.opPattern","COPY",BODY,{"derivedFrom":makeQuery(id+"F6.opPattern","COPY",BODY,{"derivedFrom":makeQuery(id+"F5.opPattern","COPY",BODY,{"derivedFrom":makeQuery(id+"F4.opPattern","COPY",BODY,{"derivedFrom":makeQuery(id+"F3.opPattern","COPY",BODY,{"derivedFrom":makeQuery(id+"F2.opPattern","COPY",BODY,{"derivedFrom":makeQuery(id+"F1.opRevolve","SWEPT_BODY",BODY,{"disambiguationData":[OSD([sQuery(id+"F0.wireOp",EDGE,"E1")])]}),"instanceName":"1"}),"instanceName":"1"}),"instanceName":"1"}),"instanceName":"1"}),"instanceName":"1"}),"instanceName":"1"}),"instanceName":"1"}),"instanceName":"1"});
            var Q1031;
            Q1031=makeQuery(id+"F12.opPattern","COPY",BODY,{"derivedFrom":makeQuery(id+"F10.opPattern","COPY",BODY,{"derivedFrom":makeQuery(id+"F8.opPattern","COPY",BODY,{"derivedFrom":makeQuery(id+"F7.opPattern","COPY",BODY,{"derivedFrom":makeQuery(id+"F1.opRevolve","SWEPT_BODY",BODY,{"disambiguationData":[OSD([sQuery(id+"F0.wireOp",EDGE,"E1")])]}),"instanceName":"1"}),"instanceName":"1"}),"instanceName":"1"}),"instanceName":"1"});
            var Q1032;
            Q1032=makeQuery(id+"F12.opPattern","COPY",BODY,{"derivedFrom":makeQuery(id+"F10.opPattern","COPY",BODY,{"derivedFrom":makeQuery(id+"F8.opPattern","COPY",BODY,{"derivedFrom":makeQuery(id+"F7.opPattern","COPY",BODY,{"derivedFrom":makeQuery(id+"F2.opPattern","COPY",BODY,{"derivedFrom":makeQuery(id+"F1.opRevolve","SWEPT_BODY",BODY,{"disambiguationData":[OSD([sQuery(id+"F0.wireOp",EDGE,"E1")])]}),"instanceName":"1"}),"instanceName":"1"}),"instanceName":"1"}),"instanceName":"1"}),"instanceName":"1"});
            var Q1033;
            Q1033=makeQuery(id+"F12.opPattern","COPY",BODY,{"derivedFrom":makeQuery(id+"F10.opPattern","COPY",BODY,{"derivedFrom":makeQuery(id+"F8.opPattern","COPY",BODY,{"derivedFrom":makeQuery(id+"F7.opPattern","COPY",BODY,{"derivedFrom":makeQuery(id+"F3.opPattern","COPY",BODY,{"derivedFrom":makeQuery(id+"F2.opPattern","COPY",BODY,{"derivedFrom":makeQuery(id+"F1.opRevolve","SWEPT_BODY",BODY,{"disambiguationData":[OSD([sQuery(id+"F0.wireOp",EDGE,"E1")])]}),"instanceName":"1"}),"instanceName":"1"}),"instanceName":"1"}),"instanceName":"1"}),"instanceName":"1"}),"instanceName":"1"});
            var Q1034;
            Q1034=makeQuery(id+"F12.opPattern","COPY",BODY,{"derivedFrom":makeQuery(id+"F10.opPattern","COPY",BODY,{"derivedFrom":makeQuery(id+"F8.opPattern","COPY",BODY,{"derivedFrom":makeQuery(id+"F7.opPattern","COPY",BODY,{"derivedFrom":makeQuery(id+"F4.opPattern","COPY",BODY,{"derivedFrom":makeQuery(id+"F1.opRevolve","SWEPT_BODY",BODY,{"disambiguationData":[OSD([sQuery(id+"F0.wireOp",EDGE,"E1")])]}),"instanceName":"1"}),"instanceName":"1"}),"instanceName":"1"}),"instanceName":"1"}),"instanceName":"1"});
            var Q1035;
            Q1035=makeQuery(id+"F12.opPattern","COPY",BODY,{"derivedFrom":makeQuery(id+"F10.opPattern","COPY",BODY,{"derivedFrom":makeQuery(id+"F8.opPattern","COPY",BODY,{"derivedFrom":makeQuery(id+"F7.opPattern","COPY",BODY,{"derivedFrom":makeQuery(id+"F4.opPattern","COPY",BODY,{"derivedFrom":makeQuery(id+"F2.opPattern","COPY",BODY,{"derivedFrom":makeQuery(id+"F1.opRevolve","SWEPT_BODY",BODY,{"disambiguationData":[OSD([sQuery(id+"F0.wireOp",EDGE,"E1")])]}),"instanceName":"1"}),"instanceName":"1"}),"instanceName":"1"}),"instanceName":"1"}),"instanceName":"1"}),"instanceName":"1"});
            var Q1036;
            Q1036=makeQuery(id+"F12.opPattern","COPY",BODY,{"derivedFrom":makeQuery(id+"F10.opPattern","COPY",BODY,{"derivedFrom":makeQuery(id+"F8.opPattern","COPY",BODY,{"derivedFrom":makeQuery(id+"F7.opPattern","COPY",BODY,{"derivedFrom":makeQuery(id+"F4.opPattern","COPY",BODY,{"derivedFrom":makeQuery(id+"F3.opPattern","COPY",BODY,{"derivedFrom":makeQuery(id+"F2.opPattern","COPY",BODY,{"derivedFrom":makeQuery(id+"F1.opRevolve","SWEPT_BODY",BODY,{"disambiguationData":[OSD([sQuery(id+"F0.wireOp",EDGE,"E1")])]}),"instanceName":"1"}),"instanceName":"1"}),"instanceName":"1"}),"instanceName":"1"}),"instanceName":"1"}),"instanceName":"1"}),"instanceName":"1"});
            var Q1037;
            Q1037=makeQuery(id+"F12.opPattern","COPY",BODY,{"derivedFrom":makeQuery(id+"F10.opPattern","COPY",BODY,{"derivedFrom":makeQuery(id+"F8.opPattern","COPY",BODY,{"derivedFrom":makeQuery(id+"F7.opPattern","COPY",BODY,{"derivedFrom":makeQuery(id+"F5.opPattern","COPY",BODY,{"derivedFrom":makeQuery(id+"F1.opRevolve","SWEPT_BODY",BODY,{"disambiguationData":[OSD([sQuery(id+"F0.wireOp",EDGE,"E1")])]}),"instanceName":"1"}),"instanceName":"1"}),"instanceName":"1"}),"instanceName":"1"}),"instanceName":"1"});
            var Q1038;
            Q1038=makeQuery(id+"F12.opPattern","COPY",BODY,{"derivedFrom":makeQuery(id+"F10.opPattern","COPY",BODY,{"derivedFrom":makeQuery(id+"F8.opPattern","COPY",BODY,{"derivedFrom":makeQuery(id+"F7.opPattern","COPY",BODY,{"derivedFrom":makeQuery(id+"F5.opPattern","COPY",BODY,{"derivedFrom":makeQuery(id+"F2.opPattern","COPY",BODY,{"derivedFrom":makeQuery(id+"F1.opRevolve","SWEPT_BODY",BODY,{"disambiguationData":[OSD([sQuery(id+"F0.wireOp",EDGE,"E1")])]}),"instanceName":"1"}),"instanceName":"1"}),"instanceName":"1"}),"instanceName":"1"}),"instanceName":"1"}),"instanceName":"1"});
            var Q1039;
            Q1039=makeQuery(id+"F12.opPattern","COPY",BODY,{"derivedFrom":makeQuery(id+"F10.opPattern","COPY",BODY,{"derivedFrom":makeQuery(id+"F8.opPattern","COPY",BODY,{"derivedFrom":makeQuery(id+"F7.opPattern","COPY",BODY,{"derivedFrom":makeQuery(id+"F5.opPattern","COPY",BODY,{"derivedFrom":makeQuery(id+"F3.opPattern","COPY",BODY,{"derivedFrom":makeQuery(id+"F2.opPattern","COPY",BODY,{"derivedFrom":makeQuery(id+"F1.opRevolve","SWEPT_BODY",BODY,{"disambiguationData":[OSD([sQuery(id+"F0.wireOp",EDGE,"E1")])]}),"instanceName":"1"}),"instanceName":"1"}),"instanceName":"1"}),"instanceName":"1"}),"instanceName":"1"}),"instanceName":"1"}),"instanceName":"1"});
            var Q1040;
            Q1040=makeQuery(id+"F12.opPattern","COPY",BODY,{"derivedFrom":makeQuery(id+"F10.opPattern","COPY",BODY,{"derivedFrom":makeQuery(id+"F8.opPattern","COPY",BODY,{"derivedFrom":makeQuery(id+"F7.opPattern","COPY",BODY,{"derivedFrom":makeQuery(id+"F5.opPattern","COPY",BODY,{"derivedFrom":makeQuery(id+"F4.opPattern","COPY",BODY,{"derivedFrom":makeQuery(id+"F1.opRevolve","SWEPT_BODY",BODY,{"disambiguationData":[OSD([sQuery(id+"F0.wireOp",EDGE,"E1")])]}),"instanceName":"1"}),"instanceName":"1"}),"instanceName":"1"}),"instanceName":"1"}),"instanceName":"1"}),"instanceName":"1"});
            var Q1041;
            Q1041=makeQuery(id+"F12.opPattern","COPY",BODY,{"derivedFrom":makeQuery(id+"F10.opPattern","COPY",BODY,{"derivedFrom":makeQuery(id+"F8.opPattern","COPY",BODY,{"derivedFrom":makeQuery(id+"F7.opPattern","COPY",BODY,{"derivedFrom":makeQuery(id+"F5.opPattern","COPY",BODY,{"derivedFrom":makeQuery(id+"F4.opPattern","COPY",BODY,{"derivedFrom":makeQuery(id+"F2.opPattern","COPY",BODY,{"derivedFrom":makeQuery(id+"F1.opRevolve","SWEPT_BODY",BODY,{"disambiguationData":[OSD([sQuery(id+"F0.wireOp",EDGE,"E1")])]}),"instanceName":"1"}),"instanceName":"1"}),"instanceName":"1"}),"instanceName":"1"}),"instanceName":"1"}),"instanceName":"1"}),"instanceName":"1"});
            var Q1042;
            Q1042=makeQuery(id+"F12.opPattern","COPY",BODY,{"derivedFrom":makeQuery(id+"F10.opPattern","COPY",BODY,{"derivedFrom":makeQuery(id+"F8.opPattern","COPY",BODY,{"derivedFrom":makeQuery(id+"F7.opPattern","COPY",BODY,{"derivedFrom":makeQuery(id+"F5.opPattern","COPY",BODY,{"derivedFrom":makeQuery(id+"F4.opPattern","COPY",BODY,{"derivedFrom":makeQuery(id+"F3.opPattern","COPY",BODY,{"derivedFrom":makeQuery(id+"F2.opPattern","COPY",BODY,{"derivedFrom":makeQuery(id+"F1.opRevolve","SWEPT_BODY",BODY,{"disambiguationData":[OSD([sQuery(id+"F0.wireOp",EDGE,"E1")])]}),"instanceName":"1"}),"instanceName":"1"}),"instanceName":"1"}),"instanceName":"1"}),"instanceName":"1"}),"instanceName":"1"}),"instanceName":"1"}),"instanceName":"1"});
            var Q1043;
            Q1043=makeQuery(id+"F12.opPattern","COPY",BODY,{"derivedFrom":makeQuery(id+"F10.opPattern","COPY",BODY,{"derivedFrom":makeQuery(id+"F8.opPattern","COPY",BODY,{"derivedFrom":makeQuery(id+"F7.opPattern","COPY",BODY,{"derivedFrom":makeQuery(id+"F6.opPattern","COPY",BODY,{"derivedFrom":makeQuery(id+"F1.opRevolve","SWEPT_BODY",BODY,{"disambiguationData":[OSD([sQuery(id+"F0.wireOp",EDGE,"E1")])]}),"instanceName":"1"}),"instanceName":"1"}),"instanceName":"1"}),"instanceName":"1"}),"instanceName":"1"});
            var Q1044;
            Q1044=makeQuery(id+"F12.opPattern","COPY",BODY,{"derivedFrom":makeQuery(id+"F10.opPattern","COPY",BODY,{"derivedFrom":makeQuery(id+"F8.opPattern","COPY",BODY,{"derivedFrom":makeQuery(id+"F7.opPattern","COPY",BODY,{"derivedFrom":makeQuery(id+"F6.opPattern","COPY",BODY,{"derivedFrom":makeQuery(id+"F2.opPattern","COPY",BODY,{"derivedFrom":makeQuery(id+"F1.opRevolve","SWEPT_BODY",BODY,{"disambiguationData":[OSD([sQuery(id+"F0.wireOp",EDGE,"E1")])]}),"instanceName":"1"}),"instanceName":"1"}),"instanceName":"1"}),"instanceName":"1"}),"instanceName":"1"}),"instanceName":"1"});
            var Q1045;
            Q1045=makeQuery(id+"F12.opPattern","COPY",BODY,{"derivedFrom":makeQuery(id+"F10.opPattern","COPY",BODY,{"derivedFrom":makeQuery(id+"F8.opPattern","COPY",BODY,{"derivedFrom":makeQuery(id+"F7.opPattern","COPY",BODY,{"derivedFrom":makeQuery(id+"F6.opPattern","COPY",BODY,{"derivedFrom":makeQuery(id+"F3.opPattern","COPY",BODY,{"derivedFrom":makeQuery(id+"F2.opPattern","COPY",BODY,{"derivedFrom":makeQuery(id+"F1.opRevolve","SWEPT_BODY",BODY,{"disambiguationData":[OSD([sQuery(id+"F0.wireOp",EDGE,"E1")])]}),"instanceName":"1"}),"instanceName":"1"}),"instanceName":"1"}),"instanceName":"1"}),"instanceName":"1"}),"instanceName":"1"}),"instanceName":"1"});
            var Q1046;
            Q1046=makeQuery(id+"F12.opPattern","COPY",BODY,{"derivedFrom":makeQuery(id+"F10.opPattern","COPY",BODY,{"derivedFrom":makeQuery(id+"F8.opPattern","COPY",BODY,{"derivedFrom":makeQuery(id+"F7.opPattern","COPY",BODY,{"derivedFrom":makeQuery(id+"F6.opPattern","COPY",BODY,{"derivedFrom":makeQuery(id+"F4.opPattern","COPY",BODY,{"derivedFrom":makeQuery(id+"F1.opRevolve","SWEPT_BODY",BODY,{"disambiguationData":[OSD([sQuery(id+"F0.wireOp",EDGE,"E1")])]}),"instanceName":"1"}),"instanceName":"1"}),"instanceName":"1"}),"instanceName":"1"}),"instanceName":"1"}),"instanceName":"1"});
            var Q1047;
            Q1047=makeQuery(id+"F12.opPattern","COPY",BODY,{"derivedFrom":makeQuery(id+"F10.opPattern","COPY",BODY,{"derivedFrom":makeQuery(id+"F8.opPattern","COPY",BODY,{"derivedFrom":makeQuery(id+"F7.opPattern","COPY",BODY,{"derivedFrom":makeQuery(id+"F6.opPattern","COPY",BODY,{"derivedFrom":makeQuery(id+"F4.opPattern","COPY",BODY,{"derivedFrom":makeQuery(id+"F2.opPattern","COPY",BODY,{"derivedFrom":makeQuery(id+"F1.opRevolve","SWEPT_BODY",BODY,{"disambiguationData":[OSD([sQuery(id+"F0.wireOp",EDGE,"E1")])]}),"instanceName":"1"}),"instanceName":"1"}),"instanceName":"1"}),"instanceName":"1"}),"instanceName":"1"}),"instanceName":"1"}),"instanceName":"1"});
            var Q1048;
            Q1048=makeQuery(id+"F12.opPattern","COPY",BODY,{"derivedFrom":makeQuery(id+"F10.opPattern","COPY",BODY,{"derivedFrom":makeQuery(id+"F8.opPattern","COPY",BODY,{"derivedFrom":makeQuery(id+"F7.opPattern","COPY",BODY,{"derivedFrom":makeQuery(id+"F6.opPattern","COPY",BODY,{"derivedFrom":makeQuery(id+"F4.opPattern","COPY",BODY,{"derivedFrom":makeQuery(id+"F3.opPattern","COPY",BODY,{"derivedFrom":makeQuery(id+"F2.opPattern","COPY",BODY,{"derivedFrom":makeQuery(id+"F1.opRevolve","SWEPT_BODY",BODY,{"disambiguationData":[OSD([sQuery(id+"F0.wireOp",EDGE,"E1")])]}),"instanceName":"1"}),"instanceName":"1"}),"instanceName":"1"}),"instanceName":"1"}),"instanceName":"1"}),"instanceName":"1"}),"instanceName":"1"}),"instanceName":"1"});
            var Q1049;
            Q1049=makeQuery(id+"F12.opPattern","COPY",BODY,{"derivedFrom":makeQuery(id+"F10.opPattern","COPY",BODY,{"derivedFrom":makeQuery(id+"F8.opPattern","COPY",BODY,{"derivedFrom":makeQuery(id+"F7.opPattern","COPY",BODY,{"derivedFrom":makeQuery(id+"F6.opPattern","COPY",BODY,{"derivedFrom":makeQuery(id+"F5.opPattern","COPY",BODY,{"derivedFrom":makeQuery(id+"F1.opRevolve","SWEPT_BODY",BODY,{"disambiguationData":[OSD([sQuery(id+"F0.wireOp",EDGE,"E1")])]}),"instanceName":"1"}),"instanceName":"1"}),"instanceName":"1"}),"instanceName":"1"}),"instanceName":"1"}),"instanceName":"1"});
            var Q1050;
            Q1050=makeQuery(id+"F12.opPattern","COPY",BODY,{"derivedFrom":makeQuery(id+"F10.opPattern","COPY",BODY,{"derivedFrom":makeQuery(id+"F8.opPattern","COPY",BODY,{"derivedFrom":makeQuery(id+"F7.opPattern","COPY",BODY,{"derivedFrom":makeQuery(id+"F6.opPattern","COPY",BODY,{"derivedFrom":makeQuery(id+"F5.opPattern","COPY",BODY,{"derivedFrom":makeQuery(id+"F2.opPattern","COPY",BODY,{"derivedFrom":makeQuery(id+"F1.opRevolve","SWEPT_BODY",BODY,{"disambiguationData":[OSD([sQuery(id+"F0.wireOp",EDGE,"E1")])]}),"instanceName":"1"}),"instanceName":"1"}),"instanceName":"1"}),"instanceName":"1"}),"instanceName":"1"}),"instanceName":"1"}),"instanceName":"1"});
            var Q1051;
            Q1051=makeQuery(id+"F12.opPattern","COPY",BODY,{"derivedFrom":makeQuery(id+"F10.opPattern","COPY",BODY,{"derivedFrom":makeQuery(id+"F8.opPattern","COPY",BODY,{"derivedFrom":makeQuery(id+"F7.opPattern","COPY",BODY,{"derivedFrom":makeQuery(id+"F6.opPattern","COPY",BODY,{"derivedFrom":makeQuery(id+"F5.opPattern","COPY",BODY,{"derivedFrom":makeQuery(id+"F3.opPattern","COPY",BODY,{"derivedFrom":makeQuery(id+"F2.opPattern","COPY",BODY,{"derivedFrom":makeQuery(id+"F1.opRevolve","SWEPT_BODY",BODY,{"disambiguationData":[OSD([sQuery(id+"F0.wireOp",EDGE,"E1")])]}),"instanceName":"1"}),"instanceName":"1"}),"instanceName":"1"}),"instanceName":"1"}),"instanceName":"1"}),"instanceName":"1"}),"instanceName":"1"}),"instanceName":"1"});
            var Q1052;
            Q1052=makeQuery(id+"F12.opPattern","COPY",BODY,{"derivedFrom":makeQuery(id+"F10.opPattern","COPY",BODY,{"derivedFrom":makeQuery(id+"F8.opPattern","COPY",BODY,{"derivedFrom":makeQuery(id+"F7.opPattern","COPY",BODY,{"derivedFrom":makeQuery(id+"F6.opPattern","COPY",BODY,{"derivedFrom":makeQuery(id+"F5.opPattern","COPY",BODY,{"derivedFrom":makeQuery(id+"F4.opPattern","COPY",BODY,{"derivedFrom":makeQuery(id+"F1.opRevolve","SWEPT_BODY",BODY,{"disambiguationData":[OSD([sQuery(id+"F0.wireOp",EDGE,"E1")])]}),"instanceName":"1"}),"instanceName":"1"}),"instanceName":"1"}),"instanceName":"1"}),"instanceName":"1"}),"instanceName":"1"}),"instanceName":"1"});
            var Q1053;
            Q1053=makeQuery(id+"F12.opPattern","COPY",BODY,{"derivedFrom":makeQuery(id+"F10.opPattern","COPY",BODY,{"derivedFrom":makeQuery(id+"F8.opPattern","COPY",BODY,{"derivedFrom":makeQuery(id+"F7.opPattern","COPY",BODY,{"derivedFrom":makeQuery(id+"F6.opPattern","COPY",BODY,{"derivedFrom":makeQuery(id+"F5.opPattern","COPY",BODY,{"derivedFrom":makeQuery(id+"F4.opPattern","COPY",BODY,{"derivedFrom":makeQuery(id+"F2.opPattern","COPY",BODY,{"derivedFrom":makeQuery(id+"F1.opRevolve","SWEPT_BODY",BODY,{"disambiguationData":[OSD([sQuery(id+"F0.wireOp",EDGE,"E1")])]}),"instanceName":"1"}),"instanceName":"1"}),"instanceName":"1"}),"instanceName":"1"}),"instanceName":"1"}),"instanceName":"1"}),"instanceName":"1"}),"instanceName":"1"});
            var Q1054;
            Q1054=makeQuery(id+"F12.opPattern","COPY",BODY,{"derivedFrom":makeQuery(id+"F10.opPattern","COPY",BODY,{"derivedFrom":makeQuery(id+"F8.opPattern","COPY",BODY,{"derivedFrom":makeQuery(id+"F7.opPattern","COPY",BODY,{"derivedFrom":makeQuery(id+"F6.opPattern","COPY",BODY,{"derivedFrom":makeQuery(id+"F5.opPattern","COPY",BODY,{"derivedFrom":makeQuery(id+"F4.opPattern","COPY",BODY,{"derivedFrom":makeQuery(id+"F3.opPattern","COPY",BODY,{"derivedFrom":makeQuery(id+"F2.opPattern","COPY",BODY,{"derivedFrom":makeQuery(id+"F1.opRevolve","SWEPT_BODY",BODY,{"disambiguationData":[OSD([sQuery(id+"F0.wireOp",EDGE,"E1")])]}),"instanceName":"1"}),"instanceName":"1"}),"instanceName":"1"}),"instanceName":"1"}),"instanceName":"1"}),"instanceName":"1"}),"instanceName":"1"}),"instanceName":"1"}),"instanceName":"1"});
            var Q1055;
            Q1055=makeQuery(id+"F12.opPattern","COPY",BODY,{"derivedFrom":makeQuery(id+"F10.opPattern","COPY",BODY,{"derivedFrom":makeQuery(id+"F9.opPattern","COPY",BODY,{"derivedFrom":makeQuery(id+"F1.opRevolve","SWEPT_BODY",BODY,{"disambiguationData":[OSD([sQuery(id+"F0.wireOp",EDGE,"E1")])]}),"instanceName":"1"}),"instanceName":"1"}),"instanceName":"1"});
            var Q1056;
            Q1056=makeQuery(id+"F12.opPattern","COPY",BODY,{"derivedFrom":makeQuery(id+"F10.opPattern","COPY",BODY,{"derivedFrom":makeQuery(id+"F9.opPattern","COPY",BODY,{"derivedFrom":makeQuery(id+"F2.opPattern","COPY",BODY,{"derivedFrom":makeQuery(id+"F1.opRevolve","SWEPT_BODY",BODY,{"disambiguationData":[OSD([sQuery(id+"F0.wireOp",EDGE,"E1")])]}),"instanceName":"1"}),"instanceName":"1"}),"instanceName":"1"}),"instanceName":"1"});
            var Q1057;
            Q1057=makeQuery(id+"F12.opPattern","COPY",BODY,{"derivedFrom":makeQuery(id+"F10.opPattern","COPY",BODY,{"derivedFrom":makeQuery(id+"F9.opPattern","COPY",BODY,{"derivedFrom":makeQuery(id+"F3.opPattern","COPY",BODY,{"derivedFrom":makeQuery(id+"F2.opPattern","COPY",BODY,{"derivedFrom":makeQuery(id+"F1.opRevolve","SWEPT_BODY",BODY,{"disambiguationData":[OSD([sQuery(id+"F0.wireOp",EDGE,"E1")])]}),"instanceName":"1"}),"instanceName":"1"}),"instanceName":"1"}),"instanceName":"1"}),"instanceName":"1"});
            var Q1058;
            Q1058=makeQuery(id+"F12.opPattern","COPY",BODY,{"derivedFrom":makeQuery(id+"F10.opPattern","COPY",BODY,{"derivedFrom":makeQuery(id+"F9.opPattern","COPY",BODY,{"derivedFrom":makeQuery(id+"F4.opPattern","COPY",BODY,{"derivedFrom":makeQuery(id+"F1.opRevolve","SWEPT_BODY",BODY,{"disambiguationData":[OSD([sQuery(id+"F0.wireOp",EDGE,"E1")])]}),"instanceName":"1"}),"instanceName":"1"}),"instanceName":"1"}),"instanceName":"1"});
            var Q1059;
            Q1059=makeQuery(id+"F12.opPattern","COPY",BODY,{"derivedFrom":makeQuery(id+"F10.opPattern","COPY",BODY,{"derivedFrom":makeQuery(id+"F9.opPattern","COPY",BODY,{"derivedFrom":makeQuery(id+"F4.opPattern","COPY",BODY,{"derivedFrom":makeQuery(id+"F2.opPattern","COPY",BODY,{"derivedFrom":makeQuery(id+"F1.opRevolve","SWEPT_BODY",BODY,{"disambiguationData":[OSD([sQuery(id+"F0.wireOp",EDGE,"E1")])]}),"instanceName":"1"}),"instanceName":"1"}),"instanceName":"1"}),"instanceName":"1"}),"instanceName":"1"});
            var Q1060;
            Q1060=makeQuery(id+"F12.opPattern","COPY",BODY,{"derivedFrom":makeQuery(id+"F10.opPattern","COPY",BODY,{"derivedFrom":makeQuery(id+"F9.opPattern","COPY",BODY,{"derivedFrom":makeQuery(id+"F4.opPattern","COPY",BODY,{"derivedFrom":makeQuery(id+"F3.opPattern","COPY",BODY,{"derivedFrom":makeQuery(id+"F2.opPattern","COPY",BODY,{"derivedFrom":makeQuery(id+"F1.opRevolve","SWEPT_BODY",BODY,{"disambiguationData":[OSD([sQuery(id+"F0.wireOp",EDGE,"E1")])]}),"instanceName":"1"}),"instanceName":"1"}),"instanceName":"1"}),"instanceName":"1"}),"instanceName":"1"}),"instanceName":"1"});
            var Q1061;
            Q1061=makeQuery(id+"F12.opPattern","COPY",BODY,{"derivedFrom":makeQuery(id+"F10.opPattern","COPY",BODY,{"derivedFrom":makeQuery(id+"F9.opPattern","COPY",BODY,{"derivedFrom":makeQuery(id+"F5.opPattern","COPY",BODY,{"derivedFrom":makeQuery(id+"F1.opRevolve","SWEPT_BODY",BODY,{"disambiguationData":[OSD([sQuery(id+"F0.wireOp",EDGE,"E1")])]}),"instanceName":"1"}),"instanceName":"1"}),"instanceName":"1"}),"instanceName":"1"});
            var Q1062;
            Q1062=makeQuery(id+"F12.opPattern","COPY",BODY,{"derivedFrom":makeQuery(id+"F10.opPattern","COPY",BODY,{"derivedFrom":makeQuery(id+"F9.opPattern","COPY",BODY,{"derivedFrom":makeQuery(id+"F5.opPattern","COPY",BODY,{"derivedFrom":makeQuery(id+"F2.opPattern","COPY",BODY,{"derivedFrom":makeQuery(id+"F1.opRevolve","SWEPT_BODY",BODY,{"disambiguationData":[OSD([sQuery(id+"F0.wireOp",EDGE,"E1")])]}),"instanceName":"1"}),"instanceName":"1"}),"instanceName":"1"}),"instanceName":"1"}),"instanceName":"1"});
            var Q1063;
            Q1063=makeQuery(id+"F12.opPattern","COPY",BODY,{"derivedFrom":makeQuery(id+"F10.opPattern","COPY",BODY,{"derivedFrom":makeQuery(id+"F9.opPattern","COPY",BODY,{"derivedFrom":makeQuery(id+"F5.opPattern","COPY",BODY,{"derivedFrom":makeQuery(id+"F3.opPattern","COPY",BODY,{"derivedFrom":makeQuery(id+"F2.opPattern","COPY",BODY,{"derivedFrom":makeQuery(id+"F1.opRevolve","SWEPT_BODY",BODY,{"disambiguationData":[OSD([sQuery(id+"F0.wireOp",EDGE,"E1")])]}),"instanceName":"1"}),"instanceName":"1"}),"instanceName":"1"}),"instanceName":"1"}),"instanceName":"1"}),"instanceName":"1"});
            var Q1064;
            Q1064=makeQuery(id+"F12.opPattern","COPY",BODY,{"derivedFrom":makeQuery(id+"F10.opPattern","COPY",BODY,{"derivedFrom":makeQuery(id+"F9.opPattern","COPY",BODY,{"derivedFrom":makeQuery(id+"F5.opPattern","COPY",BODY,{"derivedFrom":makeQuery(id+"F4.opPattern","COPY",BODY,{"derivedFrom":makeQuery(id+"F1.opRevolve","SWEPT_BODY",BODY,{"disambiguationData":[OSD([sQuery(id+"F0.wireOp",EDGE,"E1")])]}),"instanceName":"1"}),"instanceName":"1"}),"instanceName":"1"}),"instanceName":"1"}),"instanceName":"1"});
            var Q1065;
            Q1065=makeQuery(id+"F12.opPattern","COPY",BODY,{"derivedFrom":makeQuery(id+"F10.opPattern","COPY",BODY,{"derivedFrom":makeQuery(id+"F9.opPattern","COPY",BODY,{"derivedFrom":makeQuery(id+"F5.opPattern","COPY",BODY,{"derivedFrom":makeQuery(id+"F4.opPattern","COPY",BODY,{"derivedFrom":makeQuery(id+"F2.opPattern","COPY",BODY,{"derivedFrom":makeQuery(id+"F1.opRevolve","SWEPT_BODY",BODY,{"disambiguationData":[OSD([sQuery(id+"F0.wireOp",EDGE,"E1")])]}),"instanceName":"1"}),"instanceName":"1"}),"instanceName":"1"}),"instanceName":"1"}),"instanceName":"1"}),"instanceName":"1"});
            var Q1066;
            Q1066=makeQuery(id+"F12.opPattern","COPY",BODY,{"derivedFrom":makeQuery(id+"F10.opPattern","COPY",BODY,{"derivedFrom":makeQuery(id+"F9.opPattern","COPY",BODY,{"derivedFrom":makeQuery(id+"F5.opPattern","COPY",BODY,{"derivedFrom":makeQuery(id+"F4.opPattern","COPY",BODY,{"derivedFrom":makeQuery(id+"F3.opPattern","COPY",BODY,{"derivedFrom":makeQuery(id+"F2.opPattern","COPY",BODY,{"derivedFrom":makeQuery(id+"F1.opRevolve","SWEPT_BODY",BODY,{"disambiguationData":[OSD([sQuery(id+"F0.wireOp",EDGE,"E1")])]}),"instanceName":"1"}),"instanceName":"1"}),"instanceName":"1"}),"instanceName":"1"}),"instanceName":"1"}),"instanceName":"1"}),"instanceName":"1"});
            var Q1067;
            Q1067=makeQuery(id+"F12.opPattern","COPY",BODY,{"derivedFrom":makeQuery(id+"F10.opPattern","COPY",BODY,{"derivedFrom":makeQuery(id+"F9.opPattern","COPY",BODY,{"derivedFrom":makeQuery(id+"F6.opPattern","COPY",BODY,{"derivedFrom":makeQuery(id+"F1.opRevolve","SWEPT_BODY",BODY,{"disambiguationData":[OSD([sQuery(id+"F0.wireOp",EDGE,"E1")])]}),"instanceName":"1"}),"instanceName":"1"}),"instanceName":"1"}),"instanceName":"1"});
            var Q1068;
            Q1068=makeQuery(id+"F12.opPattern","COPY",BODY,{"derivedFrom":makeQuery(id+"F10.opPattern","COPY",BODY,{"derivedFrom":makeQuery(id+"F9.opPattern","COPY",BODY,{"derivedFrom":makeQuery(id+"F6.opPattern","COPY",BODY,{"derivedFrom":makeQuery(id+"F2.opPattern","COPY",BODY,{"derivedFrom":makeQuery(id+"F1.opRevolve","SWEPT_BODY",BODY,{"disambiguationData":[OSD([sQuery(id+"F0.wireOp",EDGE,"E1")])]}),"instanceName":"1"}),"instanceName":"1"}),"instanceName":"1"}),"instanceName":"1"}),"instanceName":"1"});
            var Q1069;
            Q1069=makeQuery(id+"F12.opPattern","COPY",BODY,{"derivedFrom":makeQuery(id+"F10.opPattern","COPY",BODY,{"derivedFrom":makeQuery(id+"F9.opPattern","COPY",BODY,{"derivedFrom":makeQuery(id+"F6.opPattern","COPY",BODY,{"derivedFrom":makeQuery(id+"F3.opPattern","COPY",BODY,{"derivedFrom":makeQuery(id+"F2.opPattern","COPY",BODY,{"derivedFrom":makeQuery(id+"F1.opRevolve","SWEPT_BODY",BODY,{"disambiguationData":[OSD([sQuery(id+"F0.wireOp",EDGE,"E1")])]}),"instanceName":"1"}),"instanceName":"1"}),"instanceName":"1"}),"instanceName":"1"}),"instanceName":"1"}),"instanceName":"1"});
            var Q1070;
            Q1070=makeQuery(id+"F12.opPattern","COPY",BODY,{"derivedFrom":makeQuery(id+"F10.opPattern","COPY",BODY,{"derivedFrom":makeQuery(id+"F9.opPattern","COPY",BODY,{"derivedFrom":makeQuery(id+"F6.opPattern","COPY",BODY,{"derivedFrom":makeQuery(id+"F4.opPattern","COPY",BODY,{"derivedFrom":makeQuery(id+"F1.opRevolve","SWEPT_BODY",BODY,{"disambiguationData":[OSD([sQuery(id+"F0.wireOp",EDGE,"E1")])]}),"instanceName":"1"}),"instanceName":"1"}),"instanceName":"1"}),"instanceName":"1"}),"instanceName":"1"});
            var Q1071;
            Q1071=makeQuery(id+"F12.opPattern","COPY",BODY,{"derivedFrom":makeQuery(id+"F10.opPattern","COPY",BODY,{"derivedFrom":makeQuery(id+"F9.opPattern","COPY",BODY,{"derivedFrom":makeQuery(id+"F6.opPattern","COPY",BODY,{"derivedFrom":makeQuery(id+"F4.opPattern","COPY",BODY,{"derivedFrom":makeQuery(id+"F2.opPattern","COPY",BODY,{"derivedFrom":makeQuery(id+"F1.opRevolve","SWEPT_BODY",BODY,{"disambiguationData":[OSD([sQuery(id+"F0.wireOp",EDGE,"E1")])]}),"instanceName":"1"}),"instanceName":"1"}),"instanceName":"1"}),"instanceName":"1"}),"instanceName":"1"}),"instanceName":"1"});
            var Q1072;
            Q1072=makeQuery(id+"F12.opPattern","COPY",BODY,{"derivedFrom":makeQuery(id+"F10.opPattern","COPY",BODY,{"derivedFrom":makeQuery(id+"F9.opPattern","COPY",BODY,{"derivedFrom":makeQuery(id+"F6.opPattern","COPY",BODY,{"derivedFrom":makeQuery(id+"F4.opPattern","COPY",BODY,{"derivedFrom":makeQuery(id+"F3.opPattern","COPY",BODY,{"derivedFrom":makeQuery(id+"F2.opPattern","COPY",BODY,{"derivedFrom":makeQuery(id+"F1.opRevolve","SWEPT_BODY",BODY,{"disambiguationData":[OSD([sQuery(id+"F0.wireOp",EDGE,"E1")])]}),"instanceName":"1"}),"instanceName":"1"}),"instanceName":"1"}),"instanceName":"1"}),"instanceName":"1"}),"instanceName":"1"}),"instanceName":"1"});
            var Q1073;
            Q1073=makeQuery(id+"F12.opPattern","COPY",BODY,{"derivedFrom":makeQuery(id+"F10.opPattern","COPY",BODY,{"derivedFrom":makeQuery(id+"F9.opPattern","COPY",BODY,{"derivedFrom":makeQuery(id+"F6.opPattern","COPY",BODY,{"derivedFrom":makeQuery(id+"F5.opPattern","COPY",BODY,{"derivedFrom":makeQuery(id+"F1.opRevolve","SWEPT_BODY",BODY,{"disambiguationData":[OSD([sQuery(id+"F0.wireOp",EDGE,"E1")])]}),"instanceName":"1"}),"instanceName":"1"}),"instanceName":"1"}),"instanceName":"1"}),"instanceName":"1"});
            var Q1074;
            Q1074=makeQuery(id+"F12.opPattern","COPY",BODY,{"derivedFrom":makeQuery(id+"F10.opPattern","COPY",BODY,{"derivedFrom":makeQuery(id+"F9.opPattern","COPY",BODY,{"derivedFrom":makeQuery(id+"F6.opPattern","COPY",BODY,{"derivedFrom":makeQuery(id+"F5.opPattern","COPY",BODY,{"derivedFrom":makeQuery(id+"F2.opPattern","COPY",BODY,{"derivedFrom":makeQuery(id+"F1.opRevolve","SWEPT_BODY",BODY,{"disambiguationData":[OSD([sQuery(id+"F0.wireOp",EDGE,"E1")])]}),"instanceName":"1"}),"instanceName":"1"}),"instanceName":"1"}),"instanceName":"1"}),"instanceName":"1"}),"instanceName":"1"});
            var Q1075;
            Q1075=makeQuery(id+"F12.opPattern","COPY",BODY,{"derivedFrom":makeQuery(id+"F10.opPattern","COPY",BODY,{"derivedFrom":makeQuery(id+"F9.opPattern","COPY",BODY,{"derivedFrom":makeQuery(id+"F6.opPattern","COPY",BODY,{"derivedFrom":makeQuery(id+"F5.opPattern","COPY",BODY,{"derivedFrom":makeQuery(id+"F3.opPattern","COPY",BODY,{"derivedFrom":makeQuery(id+"F2.opPattern","COPY",BODY,{"derivedFrom":makeQuery(id+"F1.opRevolve","SWEPT_BODY",BODY,{"disambiguationData":[OSD([sQuery(id+"F0.wireOp",EDGE,"E1")])]}),"instanceName":"1"}),"instanceName":"1"}),"instanceName":"1"}),"instanceName":"1"}),"instanceName":"1"}),"instanceName":"1"}),"instanceName":"1"});
            var Q1076;
            Q1076=makeQuery(id+"F12.opPattern","COPY",BODY,{"derivedFrom":makeQuery(id+"F10.opPattern","COPY",BODY,{"derivedFrom":makeQuery(id+"F9.opPattern","COPY",BODY,{"derivedFrom":makeQuery(id+"F6.opPattern","COPY",BODY,{"derivedFrom":makeQuery(id+"F5.opPattern","COPY",BODY,{"derivedFrom":makeQuery(id+"F4.opPattern","COPY",BODY,{"derivedFrom":makeQuery(id+"F1.opRevolve","SWEPT_BODY",BODY,{"disambiguationData":[OSD([sQuery(id+"F0.wireOp",EDGE,"E1")])]}),"instanceName":"1"}),"instanceName":"1"}),"instanceName":"1"}),"instanceName":"1"}),"instanceName":"1"}),"instanceName":"1"});
            var Q1077;
            Q1077=makeQuery(id+"F12.opPattern","COPY",BODY,{"derivedFrom":makeQuery(id+"F10.opPattern","COPY",BODY,{"derivedFrom":makeQuery(id+"F9.opPattern","COPY",BODY,{"derivedFrom":makeQuery(id+"F6.opPattern","COPY",BODY,{"derivedFrom":makeQuery(id+"F5.opPattern","COPY",BODY,{"derivedFrom":makeQuery(id+"F4.opPattern","COPY",BODY,{"derivedFrom":makeQuery(id+"F2.opPattern","COPY",BODY,{"derivedFrom":makeQuery(id+"F1.opRevolve","SWEPT_BODY",BODY,{"disambiguationData":[OSD([sQuery(id+"F0.wireOp",EDGE,"E1")])]}),"instanceName":"1"}),"instanceName":"1"}),"instanceName":"1"}),"instanceName":"1"}),"instanceName":"1"}),"instanceName":"1"}),"instanceName":"1"});
            var Q1078;
            Q1078=makeQuery(id+"F12.opPattern","COPY",BODY,{"derivedFrom":makeQuery(id+"F10.opPattern","COPY",BODY,{"derivedFrom":makeQuery(id+"F9.opPattern","COPY",BODY,{"derivedFrom":makeQuery(id+"F6.opPattern","COPY",BODY,{"derivedFrom":makeQuery(id+"F5.opPattern","COPY",BODY,{"derivedFrom":makeQuery(id+"F4.opPattern","COPY",BODY,{"derivedFrom":makeQuery(id+"F3.opPattern","COPY",BODY,{"derivedFrom":makeQuery(id+"F2.opPattern","COPY",BODY,{"derivedFrom":makeQuery(id+"F1.opRevolve","SWEPT_BODY",BODY,{"disambiguationData":[OSD([sQuery(id+"F0.wireOp",EDGE,"E1")])]}),"instanceName":"1"}),"instanceName":"1"}),"instanceName":"1"}),"instanceName":"1"}),"instanceName":"1"}),"instanceName":"1"}),"instanceName":"1"}),"instanceName":"1"});
            var Q1079;
            Q1079=makeQuery(id+"F12.opPattern","COPY",BODY,{"derivedFrom":makeQuery(id+"F10.opPattern","COPY",BODY,{"derivedFrom":makeQuery(id+"F9.opPattern","COPY",BODY,{"derivedFrom":makeQuery(id+"F7.opPattern","COPY",BODY,{"derivedFrom":makeQuery(id+"F1.opRevolve","SWEPT_BODY",BODY,{"disambiguationData":[OSD([sQuery(id+"F0.wireOp",EDGE,"E1")])]}),"instanceName":"1"}),"instanceName":"1"}),"instanceName":"1"}),"instanceName":"1"});
            var Q1080;
            Q1080=makeQuery(id+"F12.opPattern","COPY",BODY,{"derivedFrom":makeQuery(id+"F10.opPattern","COPY",BODY,{"derivedFrom":makeQuery(id+"F9.opPattern","COPY",BODY,{"derivedFrom":makeQuery(id+"F7.opPattern","COPY",BODY,{"derivedFrom":makeQuery(id+"F2.opPattern","COPY",BODY,{"derivedFrom":makeQuery(id+"F1.opRevolve","SWEPT_BODY",BODY,{"disambiguationData":[OSD([sQuery(id+"F0.wireOp",EDGE,"E1")])]}),"instanceName":"1"}),"instanceName":"1"}),"instanceName":"1"}),"instanceName":"1"}),"instanceName":"1"});
            var Q1081;
            Q1081=makeQuery(id+"F12.opPattern","COPY",BODY,{"derivedFrom":makeQuery(id+"F10.opPattern","COPY",BODY,{"derivedFrom":makeQuery(id+"F9.opPattern","COPY",BODY,{"derivedFrom":makeQuery(id+"F7.opPattern","COPY",BODY,{"derivedFrom":makeQuery(id+"F3.opPattern","COPY",BODY,{"derivedFrom":makeQuery(id+"F2.opPattern","COPY",BODY,{"derivedFrom":makeQuery(id+"F1.opRevolve","SWEPT_BODY",BODY,{"disambiguationData":[OSD([sQuery(id+"F0.wireOp",EDGE,"E1")])]}),"instanceName":"1"}),"instanceName":"1"}),"instanceName":"1"}),"instanceName":"1"}),"instanceName":"1"}),"instanceName":"1"});
            var Q1082;
            Q1082=makeQuery(id+"F12.opPattern","COPY",BODY,{"derivedFrom":makeQuery(id+"F10.opPattern","COPY",BODY,{"derivedFrom":makeQuery(id+"F9.opPattern","COPY",BODY,{"derivedFrom":makeQuery(id+"F7.opPattern","COPY",BODY,{"derivedFrom":makeQuery(id+"F4.opPattern","COPY",BODY,{"derivedFrom":makeQuery(id+"F1.opRevolve","SWEPT_BODY",BODY,{"disambiguationData":[OSD([sQuery(id+"F0.wireOp",EDGE,"E1")])]}),"instanceName":"1"}),"instanceName":"1"}),"instanceName":"1"}),"instanceName":"1"}),"instanceName":"1"});
            var Q1083;
            Q1083=makeQuery(id+"F12.opPattern","COPY",BODY,{"derivedFrom":makeQuery(id+"F10.opPattern","COPY",BODY,{"derivedFrom":makeQuery(id+"F9.opPattern","COPY",BODY,{"derivedFrom":makeQuery(id+"F7.opPattern","COPY",BODY,{"derivedFrom":makeQuery(id+"F4.opPattern","COPY",BODY,{"derivedFrom":makeQuery(id+"F2.opPattern","COPY",BODY,{"derivedFrom":makeQuery(id+"F1.opRevolve","SWEPT_BODY",BODY,{"disambiguationData":[OSD([sQuery(id+"F0.wireOp",EDGE,"E1")])]}),"instanceName":"1"}),"instanceName":"1"}),"instanceName":"1"}),"instanceName":"1"}),"instanceName":"1"}),"instanceName":"1"});
            var Q1084;
            Q1084=makeQuery(id+"F12.opPattern","COPY",BODY,{"derivedFrom":makeQuery(id+"F10.opPattern","COPY",BODY,{"derivedFrom":makeQuery(id+"F9.opPattern","COPY",BODY,{"derivedFrom":makeQuery(id+"F7.opPattern","COPY",BODY,{"derivedFrom":makeQuery(id+"F4.opPattern","COPY",BODY,{"derivedFrom":makeQuery(id+"F3.opPattern","COPY",BODY,{"derivedFrom":makeQuery(id+"F2.opPattern","COPY",BODY,{"derivedFrom":makeQuery(id+"F1.opRevolve","SWEPT_BODY",BODY,{"disambiguationData":[OSD([sQuery(id+"F0.wireOp",EDGE,"E1")])]}),"instanceName":"1"}),"instanceName":"1"}),"instanceName":"1"}),"instanceName":"1"}),"instanceName":"1"}),"instanceName":"1"}),"instanceName":"1"});
            var Q1085;
            Q1085=makeQuery(id+"F12.opPattern","COPY",BODY,{"derivedFrom":makeQuery(id+"F10.opPattern","COPY",BODY,{"derivedFrom":makeQuery(id+"F9.opPattern","COPY",BODY,{"derivedFrom":makeQuery(id+"F7.opPattern","COPY",BODY,{"derivedFrom":makeQuery(id+"F5.opPattern","COPY",BODY,{"derivedFrom":makeQuery(id+"F1.opRevolve","SWEPT_BODY",BODY,{"disambiguationData":[OSD([sQuery(id+"F0.wireOp",EDGE,"E1")])]}),"instanceName":"1"}),"instanceName":"1"}),"instanceName":"1"}),"instanceName":"1"}),"instanceName":"1"});
            var Q1086;
            Q1086=makeQuery(id+"F12.opPattern","COPY",BODY,{"derivedFrom":makeQuery(id+"F10.opPattern","COPY",BODY,{"derivedFrom":makeQuery(id+"F9.opPattern","COPY",BODY,{"derivedFrom":makeQuery(id+"F7.opPattern","COPY",BODY,{"derivedFrom":makeQuery(id+"F5.opPattern","COPY",BODY,{"derivedFrom":makeQuery(id+"F2.opPattern","COPY",BODY,{"derivedFrom":makeQuery(id+"F1.opRevolve","SWEPT_BODY",BODY,{"disambiguationData":[OSD([sQuery(id+"F0.wireOp",EDGE,"E1")])]}),"instanceName":"1"}),"instanceName":"1"}),"instanceName":"1"}),"instanceName":"1"}),"instanceName":"1"}),"instanceName":"1"});
            var Q1087;
            Q1087=makeQuery(id+"F12.opPattern","COPY",BODY,{"derivedFrom":makeQuery(id+"F10.opPattern","COPY",BODY,{"derivedFrom":makeQuery(id+"F9.opPattern","COPY",BODY,{"derivedFrom":makeQuery(id+"F7.opPattern","COPY",BODY,{"derivedFrom":makeQuery(id+"F5.opPattern","COPY",BODY,{"derivedFrom":makeQuery(id+"F3.opPattern","COPY",BODY,{"derivedFrom":makeQuery(id+"F2.opPattern","COPY",BODY,{"derivedFrom":makeQuery(id+"F1.opRevolve","SWEPT_BODY",BODY,{"disambiguationData":[OSD([sQuery(id+"F0.wireOp",EDGE,"E1")])]}),"instanceName":"1"}),"instanceName":"1"}),"instanceName":"1"}),"instanceName":"1"}),"instanceName":"1"}),"instanceName":"1"}),"instanceName":"1"});
            var Q1088;
            Q1088=makeQuery(id+"F12.opPattern","COPY",BODY,{"derivedFrom":makeQuery(id+"F10.opPattern","COPY",BODY,{"derivedFrom":makeQuery(id+"F9.opPattern","COPY",BODY,{"derivedFrom":makeQuery(id+"F7.opPattern","COPY",BODY,{"derivedFrom":makeQuery(id+"F5.opPattern","COPY",BODY,{"derivedFrom":makeQuery(id+"F4.opPattern","COPY",BODY,{"derivedFrom":makeQuery(id+"F1.opRevolve","SWEPT_BODY",BODY,{"disambiguationData":[OSD([sQuery(id+"F0.wireOp",EDGE,"E1")])]}),"instanceName":"1"}),"instanceName":"1"}),"instanceName":"1"}),"instanceName":"1"}),"instanceName":"1"}),"instanceName":"1"});
            var Q1089;
            Q1089=makeQuery(id+"F12.opPattern","COPY",BODY,{"derivedFrom":makeQuery(id+"F10.opPattern","COPY",BODY,{"derivedFrom":makeQuery(id+"F9.opPattern","COPY",BODY,{"derivedFrom":makeQuery(id+"F7.opPattern","COPY",BODY,{"derivedFrom":makeQuery(id+"F5.opPattern","COPY",BODY,{"derivedFrom":makeQuery(id+"F4.opPattern","COPY",BODY,{"derivedFrom":makeQuery(id+"F2.opPattern","COPY",BODY,{"derivedFrom":makeQuery(id+"F1.opRevolve","SWEPT_BODY",BODY,{"disambiguationData":[OSD([sQuery(id+"F0.wireOp",EDGE,"E1")])]}),"instanceName":"1"}),"instanceName":"1"}),"instanceName":"1"}),"instanceName":"1"}),"instanceName":"1"}),"instanceName":"1"}),"instanceName":"1"});
            var Q1090;
            Q1090=makeQuery(id+"F12.opPattern","COPY",BODY,{"derivedFrom":makeQuery(id+"F10.opPattern","COPY",BODY,{"derivedFrom":makeQuery(id+"F9.opPattern","COPY",BODY,{"derivedFrom":makeQuery(id+"F7.opPattern","COPY",BODY,{"derivedFrom":makeQuery(id+"F5.opPattern","COPY",BODY,{"derivedFrom":makeQuery(id+"F4.opPattern","COPY",BODY,{"derivedFrom":makeQuery(id+"F3.opPattern","COPY",BODY,{"derivedFrom":makeQuery(id+"F2.opPattern","COPY",BODY,{"derivedFrom":makeQuery(id+"F1.opRevolve","SWEPT_BODY",BODY,{"disambiguationData":[OSD([sQuery(id+"F0.wireOp",EDGE,"E1")])]}),"instanceName":"1"}),"instanceName":"1"}),"instanceName":"1"}),"instanceName":"1"}),"instanceName":"1"}),"instanceName":"1"}),"instanceName":"1"}),"instanceName":"1"});
            var Q1091;
            Q1091=makeQuery(id+"F12.opPattern","COPY",BODY,{"derivedFrom":makeQuery(id+"F10.opPattern","COPY",BODY,{"derivedFrom":makeQuery(id+"F9.opPattern","COPY",BODY,{"derivedFrom":makeQuery(id+"F7.opPattern","COPY",BODY,{"derivedFrom":makeQuery(id+"F6.opPattern","COPY",BODY,{"derivedFrom":makeQuery(id+"F1.opRevolve","SWEPT_BODY",BODY,{"disambiguationData":[OSD([sQuery(id+"F0.wireOp",EDGE,"E1")])]}),"instanceName":"1"}),"instanceName":"1"}),"instanceName":"1"}),"instanceName":"1"}),"instanceName":"1"});
            var Q1092;
            Q1092=makeQuery(id+"F12.opPattern","COPY",BODY,{"derivedFrom":makeQuery(id+"F10.opPattern","COPY",BODY,{"derivedFrom":makeQuery(id+"F9.opPattern","COPY",BODY,{"derivedFrom":makeQuery(id+"F7.opPattern","COPY",BODY,{"derivedFrom":makeQuery(id+"F6.opPattern","COPY",BODY,{"derivedFrom":makeQuery(id+"F2.opPattern","COPY",BODY,{"derivedFrom":makeQuery(id+"F1.opRevolve","SWEPT_BODY",BODY,{"disambiguationData":[OSD([sQuery(id+"F0.wireOp",EDGE,"E1")])]}),"instanceName":"1"}),"instanceName":"1"}),"instanceName":"1"}),"instanceName":"1"}),"instanceName":"1"}),"instanceName":"1"});
            var Q1093;
            Q1093=makeQuery(id+"F12.opPattern","COPY",BODY,{"derivedFrom":makeQuery(id+"F10.opPattern","COPY",BODY,{"derivedFrom":makeQuery(id+"F9.opPattern","COPY",BODY,{"derivedFrom":makeQuery(id+"F7.opPattern","COPY",BODY,{"derivedFrom":makeQuery(id+"F6.opPattern","COPY",BODY,{"derivedFrom":makeQuery(id+"F3.opPattern","COPY",BODY,{"derivedFrom":makeQuery(id+"F2.opPattern","COPY",BODY,{"derivedFrom":makeQuery(id+"F1.opRevolve","SWEPT_BODY",BODY,{"disambiguationData":[OSD([sQuery(id+"F0.wireOp",EDGE,"E1")])]}),"instanceName":"1"}),"instanceName":"1"}),"instanceName":"1"}),"instanceName":"1"}),"instanceName":"1"}),"instanceName":"1"}),"instanceName":"1"});
            var Q1094;
            Q1094=makeQuery(id+"F12.opPattern","COPY",BODY,{"derivedFrom":makeQuery(id+"F10.opPattern","COPY",BODY,{"derivedFrom":makeQuery(id+"F9.opPattern","COPY",BODY,{"derivedFrom":makeQuery(id+"F7.opPattern","COPY",BODY,{"derivedFrom":makeQuery(id+"F6.opPattern","COPY",BODY,{"derivedFrom":makeQuery(id+"F4.opPattern","COPY",BODY,{"derivedFrom":makeQuery(id+"F1.opRevolve","SWEPT_BODY",BODY,{"disambiguationData":[OSD([sQuery(id+"F0.wireOp",EDGE,"E1")])]}),"instanceName":"1"}),"instanceName":"1"}),"instanceName":"1"}),"instanceName":"1"}),"instanceName":"1"}),"instanceName":"1"});
            var Q1095;
            Q1095=makeQuery(id+"F12.opPattern","COPY",BODY,{"derivedFrom":makeQuery(id+"F10.opPattern","COPY",BODY,{"derivedFrom":makeQuery(id+"F9.opPattern","COPY",BODY,{"derivedFrom":makeQuery(id+"F7.opPattern","COPY",BODY,{"derivedFrom":makeQuery(id+"F6.opPattern","COPY",BODY,{"derivedFrom":makeQuery(id+"F4.opPattern","COPY",BODY,{"derivedFrom":makeQuery(id+"F2.opPattern","COPY",BODY,{"derivedFrom":makeQuery(id+"F1.opRevolve","SWEPT_BODY",BODY,{"disambiguationData":[OSD([sQuery(id+"F0.wireOp",EDGE,"E1")])]}),"instanceName":"1"}),"instanceName":"1"}),"instanceName":"1"}),"instanceName":"1"}),"instanceName":"1"}),"instanceName":"1"}),"instanceName":"1"});
            var Q1096;
            Q1096=makeQuery(id+"F12.opPattern","COPY",BODY,{"derivedFrom":makeQuery(id+"F10.opPattern","COPY",BODY,{"derivedFrom":makeQuery(id+"F9.opPattern","COPY",BODY,{"derivedFrom":makeQuery(id+"F7.opPattern","COPY",BODY,{"derivedFrom":makeQuery(id+"F6.opPattern","COPY",BODY,{"derivedFrom":makeQuery(id+"F4.opPattern","COPY",BODY,{"derivedFrom":makeQuery(id+"F3.opPattern","COPY",BODY,{"derivedFrom":makeQuery(id+"F2.opPattern","COPY",BODY,{"derivedFrom":makeQuery(id+"F1.opRevolve","SWEPT_BODY",BODY,{"disambiguationData":[OSD([sQuery(id+"F0.wireOp",EDGE,"E1")])]}),"instanceName":"1"}),"instanceName":"1"}),"instanceName":"1"}),"instanceName":"1"}),"instanceName":"1"}),"instanceName":"1"}),"instanceName":"1"}),"instanceName":"1"});
            var Q1097;
            Q1097=makeQuery(id+"F12.opPattern","COPY",BODY,{"derivedFrom":makeQuery(id+"F10.opPattern","COPY",BODY,{"derivedFrom":makeQuery(id+"F9.opPattern","COPY",BODY,{"derivedFrom":makeQuery(id+"F7.opPattern","COPY",BODY,{"derivedFrom":makeQuery(id+"F6.opPattern","COPY",BODY,{"derivedFrom":makeQuery(id+"F5.opPattern","COPY",BODY,{"derivedFrom":makeQuery(id+"F1.opRevolve","SWEPT_BODY",BODY,{"disambiguationData":[OSD([sQuery(id+"F0.wireOp",EDGE,"E1")])]}),"instanceName":"1"}),"instanceName":"1"}),"instanceName":"1"}),"instanceName":"1"}),"instanceName":"1"}),"instanceName":"1"});
            var Q1098;
            Q1098=makeQuery(id+"F12.opPattern","COPY",BODY,{"derivedFrom":makeQuery(id+"F10.opPattern","COPY",BODY,{"derivedFrom":makeQuery(id+"F9.opPattern","COPY",BODY,{"derivedFrom":makeQuery(id+"F7.opPattern","COPY",BODY,{"derivedFrom":makeQuery(id+"F6.opPattern","COPY",BODY,{"derivedFrom":makeQuery(id+"F5.opPattern","COPY",BODY,{"derivedFrom":makeQuery(id+"F2.opPattern","COPY",BODY,{"derivedFrom":makeQuery(id+"F1.opRevolve","SWEPT_BODY",BODY,{"disambiguationData":[OSD([sQuery(id+"F0.wireOp",EDGE,"E1")])]}),"instanceName":"1"}),"instanceName":"1"}),"instanceName":"1"}),"instanceName":"1"}),"instanceName":"1"}),"instanceName":"1"}),"instanceName":"1"});
            var Q1099;
            Q1099=makeQuery(id+"F12.opPattern","COPY",BODY,{"derivedFrom":makeQuery(id+"F10.opPattern","COPY",BODY,{"derivedFrom":makeQuery(id+"F9.opPattern","COPY",BODY,{"derivedFrom":makeQuery(id+"F7.opPattern","COPY",BODY,{"derivedFrom":makeQuery(id+"F6.opPattern","COPY",BODY,{"derivedFrom":makeQuery(id+"F5.opPattern","COPY",BODY,{"derivedFrom":makeQuery(id+"F3.opPattern","COPY",BODY,{"derivedFrom":makeQuery(id+"F2.opPattern","COPY",BODY,{"derivedFrom":makeQuery(id+"F1.opRevolve","SWEPT_BODY",BODY,{"disambiguationData":[OSD([sQuery(id+"F0.wireOp",EDGE,"E1")])]}),"instanceName":"1"}),"instanceName":"1"}),"instanceName":"1"}),"instanceName":"1"}),"instanceName":"1"}),"instanceName":"1"}),"instanceName":"1"}),"instanceName":"1"});
            var Q1100;
            Q1100=makeQuery(id+"F12.opPattern","COPY",BODY,{"derivedFrom":makeQuery(id+"F10.opPattern","COPY",BODY,{"derivedFrom":makeQuery(id+"F9.opPattern","COPY",BODY,{"derivedFrom":makeQuery(id+"F7.opPattern","COPY",BODY,{"derivedFrom":makeQuery(id+"F6.opPattern","COPY",BODY,{"derivedFrom":makeQuery(id+"F5.opPattern","COPY",BODY,{"derivedFrom":makeQuery(id+"F4.opPattern","COPY",BODY,{"derivedFrom":makeQuery(id+"F1.opRevolve","SWEPT_BODY",BODY,{"disambiguationData":[OSD([sQuery(id+"F0.wireOp",EDGE,"E1")])]}),"instanceName":"1"}),"instanceName":"1"}),"instanceName":"1"}),"instanceName":"1"}),"instanceName":"1"}),"instanceName":"1"}),"instanceName":"1"});
            var Q1101;
            Q1101=makeQuery(id+"F12.opPattern","COPY",BODY,{"derivedFrom":makeQuery(id+"F10.opPattern","COPY",BODY,{"derivedFrom":makeQuery(id+"F9.opPattern","COPY",BODY,{"derivedFrom":makeQuery(id+"F7.opPattern","COPY",BODY,{"derivedFrom":makeQuery(id+"F6.opPattern","COPY",BODY,{"derivedFrom":makeQuery(id+"F5.opPattern","COPY",BODY,{"derivedFrom":makeQuery(id+"F4.opPattern","COPY",BODY,{"derivedFrom":makeQuery(id+"F2.opPattern","COPY",BODY,{"derivedFrom":makeQuery(id+"F1.opRevolve","SWEPT_BODY",BODY,{"disambiguationData":[OSD([sQuery(id+"F0.wireOp",EDGE,"E1")])]}),"instanceName":"1"}),"instanceName":"1"}),"instanceName":"1"}),"instanceName":"1"}),"instanceName":"1"}),"instanceName":"1"}),"instanceName":"1"}),"instanceName":"1"});
            var Q1102;
            Q1102=makeQuery(id+"F12.opPattern","COPY",BODY,{"derivedFrom":makeQuery(id+"F10.opPattern","COPY",BODY,{"derivedFrom":makeQuery(id+"F9.opPattern","COPY",BODY,{"derivedFrom":makeQuery(id+"F7.opPattern","COPY",BODY,{"derivedFrom":makeQuery(id+"F6.opPattern","COPY",BODY,{"derivedFrom":makeQuery(id+"F5.opPattern","COPY",BODY,{"derivedFrom":makeQuery(id+"F4.opPattern","COPY",BODY,{"derivedFrom":makeQuery(id+"F3.opPattern","COPY",BODY,{"derivedFrom":makeQuery(id+"F2.opPattern","COPY",BODY,{"derivedFrom":makeQuery(id+"F1.opRevolve","SWEPT_BODY",BODY,{"disambiguationData":[OSD([sQuery(id+"F0.wireOp",EDGE,"E1")])]}),"instanceName":"1"}),"instanceName":"1"}),"instanceName":"1"}),"instanceName":"1"}),"instanceName":"1"}),"instanceName":"1"}),"instanceName":"1"}),"instanceName":"1"}),"instanceName":"1"});
            var Q1103;
            Q1103=makeQuery(id+"F12.opPattern","COPY",BODY,{"derivedFrom":makeQuery(id+"F10.opPattern","COPY",BODY,{"derivedFrom":makeQuery(id+"F9.opPattern","COPY",BODY,{"derivedFrom":makeQuery(id+"F8.opPattern","COPY",BODY,{"derivedFrom":makeQuery(id+"F1.opRevolve","SWEPT_BODY",BODY,{"disambiguationData":[OSD([sQuery(id+"F0.wireOp",EDGE,"E1")])]}),"instanceName":"1"}),"instanceName":"1"}),"instanceName":"1"}),"instanceName":"1"});
            var Q1104;
            Q1104=makeQuery(id+"F12.opPattern","COPY",BODY,{"derivedFrom":makeQuery(id+"F10.opPattern","COPY",BODY,{"derivedFrom":makeQuery(id+"F9.opPattern","COPY",BODY,{"derivedFrom":makeQuery(id+"F8.opPattern","COPY",BODY,{"derivedFrom":makeQuery(id+"F2.opPattern","COPY",BODY,{"derivedFrom":makeQuery(id+"F1.opRevolve","SWEPT_BODY",BODY,{"disambiguationData":[OSD([sQuery(id+"F0.wireOp",EDGE,"E1")])]}),"instanceName":"1"}),"instanceName":"1"}),"instanceName":"1"}),"instanceName":"1"}),"instanceName":"1"});
            var Q1105;
            Q1105=makeQuery(id+"F12.opPattern","COPY",BODY,{"derivedFrom":makeQuery(id+"F10.opPattern","COPY",BODY,{"derivedFrom":makeQuery(id+"F9.opPattern","COPY",BODY,{"derivedFrom":makeQuery(id+"F8.opPattern","COPY",BODY,{"derivedFrom":makeQuery(id+"F3.opPattern","COPY",BODY,{"derivedFrom":makeQuery(id+"F2.opPattern","COPY",BODY,{"derivedFrom":makeQuery(id+"F1.opRevolve","SWEPT_BODY",BODY,{"disambiguationData":[OSD([sQuery(id+"F0.wireOp",EDGE,"E1")])]}),"instanceName":"1"}),"instanceName":"1"}),"instanceName":"1"}),"instanceName":"1"}),"instanceName":"1"}),"instanceName":"1"});
            var Q1106;
            Q1106=makeQuery(id+"F12.opPattern","COPY",BODY,{"derivedFrom":makeQuery(id+"F10.opPattern","COPY",BODY,{"derivedFrom":makeQuery(id+"F9.opPattern","COPY",BODY,{"derivedFrom":makeQuery(id+"F8.opPattern","COPY",BODY,{"derivedFrom":makeQuery(id+"F4.opPattern","COPY",BODY,{"derivedFrom":makeQuery(id+"F1.opRevolve","SWEPT_BODY",BODY,{"disambiguationData":[OSD([sQuery(id+"F0.wireOp",EDGE,"E1")])]}),"instanceName":"1"}),"instanceName":"1"}),"instanceName":"1"}),"instanceName":"1"}),"instanceName":"1"});
            var Q1107;
            Q1107=makeQuery(id+"F12.opPattern","COPY",BODY,{"derivedFrom":makeQuery(id+"F10.opPattern","COPY",BODY,{"derivedFrom":makeQuery(id+"F9.opPattern","COPY",BODY,{"derivedFrom":makeQuery(id+"F8.opPattern","COPY",BODY,{"derivedFrom":makeQuery(id+"F4.opPattern","COPY",BODY,{"derivedFrom":makeQuery(id+"F2.opPattern","COPY",BODY,{"derivedFrom":makeQuery(id+"F1.opRevolve","SWEPT_BODY",BODY,{"disambiguationData":[OSD([sQuery(id+"F0.wireOp",EDGE,"E1")])]}),"instanceName":"1"}),"instanceName":"1"}),"instanceName":"1"}),"instanceName":"1"}),"instanceName":"1"}),"instanceName":"1"});
            var Q1108;
            Q1108=makeQuery(id+"F12.opPattern","COPY",BODY,{"derivedFrom":makeQuery(id+"F10.opPattern","COPY",BODY,{"derivedFrom":makeQuery(id+"F9.opPattern","COPY",BODY,{"derivedFrom":makeQuery(id+"F8.opPattern","COPY",BODY,{"derivedFrom":makeQuery(id+"F4.opPattern","COPY",BODY,{"derivedFrom":makeQuery(id+"F3.opPattern","COPY",BODY,{"derivedFrom":makeQuery(id+"F2.opPattern","COPY",BODY,{"derivedFrom":makeQuery(id+"F1.opRevolve","SWEPT_BODY",BODY,{"disambiguationData":[OSD([sQuery(id+"F0.wireOp",EDGE,"E1")])]}),"instanceName":"1"}),"instanceName":"1"}),"instanceName":"1"}),"instanceName":"1"}),"instanceName":"1"}),"instanceName":"1"}),"instanceName":"1"});
            var Q1109;
            Q1109=makeQuery(id+"F12.opPattern","COPY",BODY,{"derivedFrom":makeQuery(id+"F10.opPattern","COPY",BODY,{"derivedFrom":makeQuery(id+"F9.opPattern","COPY",BODY,{"derivedFrom":makeQuery(id+"F8.opPattern","COPY",BODY,{"derivedFrom":makeQuery(id+"F5.opPattern","COPY",BODY,{"derivedFrom":makeQuery(id+"F1.opRevolve","SWEPT_BODY",BODY,{"disambiguationData":[OSD([sQuery(id+"F0.wireOp",EDGE,"E1")])]}),"instanceName":"1"}),"instanceName":"1"}),"instanceName":"1"}),"instanceName":"1"}),"instanceName":"1"});
            var Q1110;
            Q1110=makeQuery(id+"F12.opPattern","COPY",BODY,{"derivedFrom":makeQuery(id+"F10.opPattern","COPY",BODY,{"derivedFrom":makeQuery(id+"F9.opPattern","COPY",BODY,{"derivedFrom":makeQuery(id+"F8.opPattern","COPY",BODY,{"derivedFrom":makeQuery(id+"F5.opPattern","COPY",BODY,{"derivedFrom":makeQuery(id+"F2.opPattern","COPY",BODY,{"derivedFrom":makeQuery(id+"F1.opRevolve","SWEPT_BODY",BODY,{"disambiguationData":[OSD([sQuery(id+"F0.wireOp",EDGE,"E1")])]}),"instanceName":"1"}),"instanceName":"1"}),"instanceName":"1"}),"instanceName":"1"}),"instanceName":"1"}),"instanceName":"1"});
            var Q1111;
            Q1111=makeQuery(id+"F12.opPattern","COPY",BODY,{"derivedFrom":makeQuery(id+"F10.opPattern","COPY",BODY,{"derivedFrom":makeQuery(id+"F9.opPattern","COPY",BODY,{"derivedFrom":makeQuery(id+"F8.opPattern","COPY",BODY,{"derivedFrom":makeQuery(id+"F5.opPattern","COPY",BODY,{"derivedFrom":makeQuery(id+"F3.opPattern","COPY",BODY,{"derivedFrom":makeQuery(id+"F2.opPattern","COPY",BODY,{"derivedFrom":makeQuery(id+"F1.opRevolve","SWEPT_BODY",BODY,{"disambiguationData":[OSD([sQuery(id+"F0.wireOp",EDGE,"E1")])]}),"instanceName":"1"}),"instanceName":"1"}),"instanceName":"1"}),"instanceName":"1"}),"instanceName":"1"}),"instanceName":"1"}),"instanceName":"1"});
            var Q1112;
            Q1112=makeQuery(id+"F12.opPattern","COPY",BODY,{"derivedFrom":makeQuery(id+"F10.opPattern","COPY",BODY,{"derivedFrom":makeQuery(id+"F9.opPattern","COPY",BODY,{"derivedFrom":makeQuery(id+"F8.opPattern","COPY",BODY,{"derivedFrom":makeQuery(id+"F5.opPattern","COPY",BODY,{"derivedFrom":makeQuery(id+"F4.opPattern","COPY",BODY,{"derivedFrom":makeQuery(id+"F1.opRevolve","SWEPT_BODY",BODY,{"disambiguationData":[OSD([sQuery(id+"F0.wireOp",EDGE,"E1")])]}),"instanceName":"1"}),"instanceName":"1"}),"instanceName":"1"}),"instanceName":"1"}),"instanceName":"1"}),"instanceName":"1"});
            var Q1113;
            Q1113=makeQuery(id+"F12.opPattern","COPY",BODY,{"derivedFrom":makeQuery(id+"F10.opPattern","COPY",BODY,{"derivedFrom":makeQuery(id+"F9.opPattern","COPY",BODY,{"derivedFrom":makeQuery(id+"F8.opPattern","COPY",BODY,{"derivedFrom":makeQuery(id+"F5.opPattern","COPY",BODY,{"derivedFrom":makeQuery(id+"F4.opPattern","COPY",BODY,{"derivedFrom":makeQuery(id+"F2.opPattern","COPY",BODY,{"derivedFrom":makeQuery(id+"F1.opRevolve","SWEPT_BODY",BODY,{"disambiguationData":[OSD([sQuery(id+"F0.wireOp",EDGE,"E1")])]}),"instanceName":"1"}),"instanceName":"1"}),"instanceName":"1"}),"instanceName":"1"}),"instanceName":"1"}),"instanceName":"1"}),"instanceName":"1"});
            var Q1114;
            Q1114=makeQuery(id+"F12.opPattern","COPY",BODY,{"derivedFrom":makeQuery(id+"F10.opPattern","COPY",BODY,{"derivedFrom":makeQuery(id+"F9.opPattern","COPY",BODY,{"derivedFrom":makeQuery(id+"F8.opPattern","COPY",BODY,{"derivedFrom":makeQuery(id+"F5.opPattern","COPY",BODY,{"derivedFrom":makeQuery(id+"F4.opPattern","COPY",BODY,{"derivedFrom":makeQuery(id+"F3.opPattern","COPY",BODY,{"derivedFrom":makeQuery(id+"F2.opPattern","COPY",BODY,{"derivedFrom":makeQuery(id+"F1.opRevolve","SWEPT_BODY",BODY,{"disambiguationData":[OSD([sQuery(id+"F0.wireOp",EDGE,"E1")])]}),"instanceName":"1"}),"instanceName":"1"}),"instanceName":"1"}),"instanceName":"1"}),"instanceName":"1"}),"instanceName":"1"}),"instanceName":"1"}),"instanceName":"1"});
            var Q1115;
            Q1115=makeQuery(id+"F12.opPattern","COPY",BODY,{"derivedFrom":makeQuery(id+"F10.opPattern","COPY",BODY,{"derivedFrom":makeQuery(id+"F9.opPattern","COPY",BODY,{"derivedFrom":makeQuery(id+"F8.opPattern","COPY",BODY,{"derivedFrom":makeQuery(id+"F6.opPattern","COPY",BODY,{"derivedFrom":makeQuery(id+"F1.opRevolve","SWEPT_BODY",BODY,{"disambiguationData":[OSD([sQuery(id+"F0.wireOp",EDGE,"E1")])]}),"instanceName":"1"}),"instanceName":"1"}),"instanceName":"1"}),"instanceName":"1"}),"instanceName":"1"});
            var Q1116;
            Q1116=makeQuery(id+"F12.opPattern","COPY",BODY,{"derivedFrom":makeQuery(id+"F10.opPattern","COPY",BODY,{"derivedFrom":makeQuery(id+"F9.opPattern","COPY",BODY,{"derivedFrom":makeQuery(id+"F8.opPattern","COPY",BODY,{"derivedFrom":makeQuery(id+"F6.opPattern","COPY",BODY,{"derivedFrom":makeQuery(id+"F2.opPattern","COPY",BODY,{"derivedFrom":makeQuery(id+"F1.opRevolve","SWEPT_BODY",BODY,{"disambiguationData":[OSD([sQuery(id+"F0.wireOp",EDGE,"E1")])]}),"instanceName":"1"}),"instanceName":"1"}),"instanceName":"1"}),"instanceName":"1"}),"instanceName":"1"}),"instanceName":"1"});
            var Q1117;
            Q1117=makeQuery(id+"F12.opPattern","COPY",BODY,{"derivedFrom":makeQuery(id+"F10.opPattern","COPY",BODY,{"derivedFrom":makeQuery(id+"F9.opPattern","COPY",BODY,{"derivedFrom":makeQuery(id+"F8.opPattern","COPY",BODY,{"derivedFrom":makeQuery(id+"F6.opPattern","COPY",BODY,{"derivedFrom":makeQuery(id+"F3.opPattern","COPY",BODY,{"derivedFrom":makeQuery(id+"F2.opPattern","COPY",BODY,{"derivedFrom":makeQuery(id+"F1.opRevolve","SWEPT_BODY",BODY,{"disambiguationData":[OSD([sQuery(id+"F0.wireOp",EDGE,"E1")])]}),"instanceName":"1"}),"instanceName":"1"}),"instanceName":"1"}),"instanceName":"1"}),"instanceName":"1"}),"instanceName":"1"}),"instanceName":"1"});
            var Q1118;
            Q1118=makeQuery(id+"F12.opPattern","COPY",BODY,{"derivedFrom":makeQuery(id+"F10.opPattern","COPY",BODY,{"derivedFrom":makeQuery(id+"F9.opPattern","COPY",BODY,{"derivedFrom":makeQuery(id+"F8.opPattern","COPY",BODY,{"derivedFrom":makeQuery(id+"F6.opPattern","COPY",BODY,{"derivedFrom":makeQuery(id+"F4.opPattern","COPY",BODY,{"derivedFrom":makeQuery(id+"F1.opRevolve","SWEPT_BODY",BODY,{"disambiguationData":[OSD([sQuery(id+"F0.wireOp",EDGE,"E1")])]}),"instanceName":"1"}),"instanceName":"1"}),"instanceName":"1"}),"instanceName":"1"}),"instanceName":"1"}),"instanceName":"1"});
            var Q1119;
            Q1119=makeQuery(id+"F12.opPattern","COPY",BODY,{"derivedFrom":makeQuery(id+"F10.opPattern","COPY",BODY,{"derivedFrom":makeQuery(id+"F9.opPattern","COPY",BODY,{"derivedFrom":makeQuery(id+"F8.opPattern","COPY",BODY,{"derivedFrom":makeQuery(id+"F6.opPattern","COPY",BODY,{"derivedFrom":makeQuery(id+"F4.opPattern","COPY",BODY,{"derivedFrom":makeQuery(id+"F2.opPattern","COPY",BODY,{"derivedFrom":makeQuery(id+"F1.opRevolve","SWEPT_BODY",BODY,{"disambiguationData":[OSD([sQuery(id+"F0.wireOp",EDGE,"E1")])]}),"instanceName":"1"}),"instanceName":"1"}),"instanceName":"1"}),"instanceName":"1"}),"instanceName":"1"}),"instanceName":"1"}),"instanceName":"1"});
            var Q1120;
            Q1120=makeQuery(id+"F12.opPattern","COPY",BODY,{"derivedFrom":makeQuery(id+"F10.opPattern","COPY",BODY,{"derivedFrom":makeQuery(id+"F9.opPattern","COPY",BODY,{"derivedFrom":makeQuery(id+"F8.opPattern","COPY",BODY,{"derivedFrom":makeQuery(id+"F6.opPattern","COPY",BODY,{"derivedFrom":makeQuery(id+"F4.opPattern","COPY",BODY,{"derivedFrom":makeQuery(id+"F3.opPattern","COPY",BODY,{"derivedFrom":makeQuery(id+"F2.opPattern","COPY",BODY,{"derivedFrom":makeQuery(id+"F1.opRevolve","SWEPT_BODY",BODY,{"disambiguationData":[OSD([sQuery(id+"F0.wireOp",EDGE,"E1")])]}),"instanceName":"1"}),"instanceName":"1"}),"instanceName":"1"}),"instanceName":"1"}),"instanceName":"1"}),"instanceName":"1"}),"instanceName":"1"}),"instanceName":"1"});
            var Q1121;
            Q1121=makeQuery(id+"F12.opPattern","COPY",BODY,{"derivedFrom":makeQuery(id+"F10.opPattern","COPY",BODY,{"derivedFrom":makeQuery(id+"F9.opPattern","COPY",BODY,{"derivedFrom":makeQuery(id+"F8.opPattern","COPY",BODY,{"derivedFrom":makeQuery(id+"F6.opPattern","COPY",BODY,{"derivedFrom":makeQuery(id+"F5.opPattern","COPY",BODY,{"derivedFrom":makeQuery(id+"F1.opRevolve","SWEPT_BODY",BODY,{"disambiguationData":[OSD([sQuery(id+"F0.wireOp",EDGE,"E1")])]}),"instanceName":"1"}),"instanceName":"1"}),"instanceName":"1"}),"instanceName":"1"}),"instanceName":"1"}),"instanceName":"1"});
            var Q1122;
            Q1122=makeQuery(id+"F12.opPattern","COPY",BODY,{"derivedFrom":makeQuery(id+"F10.opPattern","COPY",BODY,{"derivedFrom":makeQuery(id+"F9.opPattern","COPY",BODY,{"derivedFrom":makeQuery(id+"F8.opPattern","COPY",BODY,{"derivedFrom":makeQuery(id+"F6.opPattern","COPY",BODY,{"derivedFrom":makeQuery(id+"F5.opPattern","COPY",BODY,{"derivedFrom":makeQuery(id+"F2.opPattern","COPY",BODY,{"derivedFrom":makeQuery(id+"F1.opRevolve","SWEPT_BODY",BODY,{"disambiguationData":[OSD([sQuery(id+"F0.wireOp",EDGE,"E1")])]}),"instanceName":"1"}),"instanceName":"1"}),"instanceName":"1"}),"instanceName":"1"}),"instanceName":"1"}),"instanceName":"1"}),"instanceName":"1"});
            var Q1123;
            Q1123=makeQuery(id+"F12.opPattern","COPY",BODY,{"derivedFrom":makeQuery(id+"F10.opPattern","COPY",BODY,{"derivedFrom":makeQuery(id+"F9.opPattern","COPY",BODY,{"derivedFrom":makeQuery(id+"F8.opPattern","COPY",BODY,{"derivedFrom":makeQuery(id+"F6.opPattern","COPY",BODY,{"derivedFrom":makeQuery(id+"F5.opPattern","COPY",BODY,{"derivedFrom":makeQuery(id+"F3.opPattern","COPY",BODY,{"derivedFrom":makeQuery(id+"F2.opPattern","COPY",BODY,{"derivedFrom":makeQuery(id+"F1.opRevolve","SWEPT_BODY",BODY,{"disambiguationData":[OSD([sQuery(id+"F0.wireOp",EDGE,"E1")])]}),"instanceName":"1"}),"instanceName":"1"}),"instanceName":"1"}),"instanceName":"1"}),"instanceName":"1"}),"instanceName":"1"}),"instanceName":"1"}),"instanceName":"1"});
            var Q1124;
            Q1124=makeQuery(id+"F12.opPattern","COPY",BODY,{"derivedFrom":makeQuery(id+"F10.opPattern","COPY",BODY,{"derivedFrom":makeQuery(id+"F9.opPattern","COPY",BODY,{"derivedFrom":makeQuery(id+"F8.opPattern","COPY",BODY,{"derivedFrom":makeQuery(id+"F6.opPattern","COPY",BODY,{"derivedFrom":makeQuery(id+"F5.opPattern","COPY",BODY,{"derivedFrom":makeQuery(id+"F4.opPattern","COPY",BODY,{"derivedFrom":makeQuery(id+"F1.opRevolve","SWEPT_BODY",BODY,{"disambiguationData":[OSD([sQuery(id+"F0.wireOp",EDGE,"E1")])]}),"instanceName":"1"}),"instanceName":"1"}),"instanceName":"1"}),"instanceName":"1"}),"instanceName":"1"}),"instanceName":"1"}),"instanceName":"1"});
            var Q1125;
            Q1125=makeQuery(id+"F12.opPattern","COPY",BODY,{"derivedFrom":makeQuery(id+"F10.opPattern","COPY",BODY,{"derivedFrom":makeQuery(id+"F9.opPattern","COPY",BODY,{"derivedFrom":makeQuery(id+"F8.opPattern","COPY",BODY,{"derivedFrom":makeQuery(id+"F6.opPattern","COPY",BODY,{"derivedFrom":makeQuery(id+"F5.opPattern","COPY",BODY,{"derivedFrom":makeQuery(id+"F4.opPattern","COPY",BODY,{"derivedFrom":makeQuery(id+"F2.opPattern","COPY",BODY,{"derivedFrom":makeQuery(id+"F1.opRevolve","SWEPT_BODY",BODY,{"disambiguationData":[OSD([sQuery(id+"F0.wireOp",EDGE,"E1")])]}),"instanceName":"1"}),"instanceName":"1"}),"instanceName":"1"}),"instanceName":"1"}),"instanceName":"1"}),"instanceName":"1"}),"instanceName":"1"}),"instanceName":"1"});
            var Q1126;
            Q1126=makeQuery(id+"F12.opPattern","COPY",BODY,{"derivedFrom":makeQuery(id+"F10.opPattern","COPY",BODY,{"derivedFrom":makeQuery(id+"F9.opPattern","COPY",BODY,{"derivedFrom":makeQuery(id+"F8.opPattern","COPY",BODY,{"derivedFrom":makeQuery(id+"F6.opPattern","COPY",BODY,{"derivedFrom":makeQuery(id+"F5.opPattern","COPY",BODY,{"derivedFrom":makeQuery(id+"F4.opPattern","COPY",BODY,{"derivedFrom":makeQuery(id+"F3.opPattern","COPY",BODY,{"derivedFrom":makeQuery(id+"F2.opPattern","COPY",BODY,{"derivedFrom":makeQuery(id+"F1.opRevolve","SWEPT_BODY",BODY,{"disambiguationData":[OSD([sQuery(id+"F0.wireOp",EDGE,"E1")])]}),"instanceName":"1"}),"instanceName":"1"}),"instanceName":"1"}),"instanceName":"1"}),"instanceName":"1"}),"instanceName":"1"}),"instanceName":"1"}),"instanceName":"1"}),"instanceName":"1"});
            var Q1127;
            Q1127=makeQuery(id+"F12.opPattern","COPY",BODY,{"derivedFrom":makeQuery(id+"F10.opPattern","COPY",BODY,{"derivedFrom":makeQuery(id+"F9.opPattern","COPY",BODY,{"derivedFrom":makeQuery(id+"F8.opPattern","COPY",BODY,{"derivedFrom":makeQuery(id+"F7.opPattern","COPY",BODY,{"derivedFrom":makeQuery(id+"F1.opRevolve","SWEPT_BODY",BODY,{"disambiguationData":[OSD([sQuery(id+"F0.wireOp",EDGE,"E1")])]}),"instanceName":"1"}),"instanceName":"1"}),"instanceName":"1"}),"instanceName":"1"}),"instanceName":"1"});
            var Q1128;
            Q1128=makeQuery(id+"F12.opPattern","COPY",BODY,{"derivedFrom":makeQuery(id+"F10.opPattern","COPY",BODY,{"derivedFrom":makeQuery(id+"F9.opPattern","COPY",BODY,{"derivedFrom":makeQuery(id+"F8.opPattern","COPY",BODY,{"derivedFrom":makeQuery(id+"F7.opPattern","COPY",BODY,{"derivedFrom":makeQuery(id+"F2.opPattern","COPY",BODY,{"derivedFrom":makeQuery(id+"F1.opRevolve","SWEPT_BODY",BODY,{"disambiguationData":[OSD([sQuery(id+"F0.wireOp",EDGE,"E1")])]}),"instanceName":"1"}),"instanceName":"1"}),"instanceName":"1"}),"instanceName":"1"}),"instanceName":"1"}),"instanceName":"1"});
            var Q1129;
            Q1129=makeQuery(id+"F12.opPattern","COPY",BODY,{"derivedFrom":makeQuery(id+"F10.opPattern","COPY",BODY,{"derivedFrom":makeQuery(id+"F9.opPattern","COPY",BODY,{"derivedFrom":makeQuery(id+"F8.opPattern","COPY",BODY,{"derivedFrom":makeQuery(id+"F7.opPattern","COPY",BODY,{"derivedFrom":makeQuery(id+"F3.opPattern","COPY",BODY,{"derivedFrom":makeQuery(id+"F2.opPattern","COPY",BODY,{"derivedFrom":makeQuery(id+"F1.opRevolve","SWEPT_BODY",BODY,{"disambiguationData":[OSD([sQuery(id+"F0.wireOp",EDGE,"E1")])]}),"instanceName":"1"}),"instanceName":"1"}),"instanceName":"1"}),"instanceName":"1"}),"instanceName":"1"}),"instanceName":"1"}),"instanceName":"1"});
            var Q1130;
            Q1130=makeQuery(id+"F12.opPattern","COPY",BODY,{"derivedFrom":makeQuery(id+"F10.opPattern","COPY",BODY,{"derivedFrom":makeQuery(id+"F9.opPattern","COPY",BODY,{"derivedFrom":makeQuery(id+"F8.opPattern","COPY",BODY,{"derivedFrom":makeQuery(id+"F7.opPattern","COPY",BODY,{"derivedFrom":makeQuery(id+"F4.opPattern","COPY",BODY,{"derivedFrom":makeQuery(id+"F1.opRevolve","SWEPT_BODY",BODY,{"disambiguationData":[OSD([sQuery(id+"F0.wireOp",EDGE,"E1")])]}),"instanceName":"1"}),"instanceName":"1"}),"instanceName":"1"}),"instanceName":"1"}),"instanceName":"1"}),"instanceName":"1"});
            var Q1131;
            Q1131=makeQuery(id+"F12.opPattern","COPY",BODY,{"derivedFrom":makeQuery(id+"F10.opPattern","COPY",BODY,{"derivedFrom":makeQuery(id+"F9.opPattern","COPY",BODY,{"derivedFrom":makeQuery(id+"F8.opPattern","COPY",BODY,{"derivedFrom":makeQuery(id+"F7.opPattern","COPY",BODY,{"derivedFrom":makeQuery(id+"F4.opPattern","COPY",BODY,{"derivedFrom":makeQuery(id+"F2.opPattern","COPY",BODY,{"derivedFrom":makeQuery(id+"F1.opRevolve","SWEPT_BODY",BODY,{"disambiguationData":[OSD([sQuery(id+"F0.wireOp",EDGE,"E1")])]}),"instanceName":"1"}),"instanceName":"1"}),"instanceName":"1"}),"instanceName":"1"}),"instanceName":"1"}),"instanceName":"1"}),"instanceName":"1"});
            var Q1132;
            Q1132=makeQuery(id+"F12.opPattern","COPY",BODY,{"derivedFrom":makeQuery(id+"F10.opPattern","COPY",BODY,{"derivedFrom":makeQuery(id+"F9.opPattern","COPY",BODY,{"derivedFrom":makeQuery(id+"F8.opPattern","COPY",BODY,{"derivedFrom":makeQuery(id+"F7.opPattern","COPY",BODY,{"derivedFrom":makeQuery(id+"F4.opPattern","COPY",BODY,{"derivedFrom":makeQuery(id+"F3.opPattern","COPY",BODY,{"derivedFrom":makeQuery(id+"F2.opPattern","COPY",BODY,{"derivedFrom":makeQuery(id+"F1.opRevolve","SWEPT_BODY",BODY,{"disambiguationData":[OSD([sQuery(id+"F0.wireOp",EDGE,"E1")])]}),"instanceName":"1"}),"instanceName":"1"}),"instanceName":"1"}),"instanceName":"1"}),"instanceName":"1"}),"instanceName":"1"}),"instanceName":"1"}),"instanceName":"1"});
            var Q1133;
            Q1133=makeQuery(id+"F12.opPattern","COPY",BODY,{"derivedFrom":makeQuery(id+"F10.opPattern","COPY",BODY,{"derivedFrom":makeQuery(id+"F9.opPattern","COPY",BODY,{"derivedFrom":makeQuery(id+"F8.opPattern","COPY",BODY,{"derivedFrom":makeQuery(id+"F7.opPattern","COPY",BODY,{"derivedFrom":makeQuery(id+"F5.opPattern","COPY",BODY,{"derivedFrom":makeQuery(id+"F1.opRevolve","SWEPT_BODY",BODY,{"disambiguationData":[OSD([sQuery(id+"F0.wireOp",EDGE,"E1")])]}),"instanceName":"1"}),"instanceName":"1"}),"instanceName":"1"}),"instanceName":"1"}),"instanceName":"1"}),"instanceName":"1"});
            var Q1134;
            Q1134=makeQuery(id+"F12.opPattern","COPY",BODY,{"derivedFrom":makeQuery(id+"F10.opPattern","COPY",BODY,{"derivedFrom":makeQuery(id+"F9.opPattern","COPY",BODY,{"derivedFrom":makeQuery(id+"F8.opPattern","COPY",BODY,{"derivedFrom":makeQuery(id+"F7.opPattern","COPY",BODY,{"derivedFrom":makeQuery(id+"F5.opPattern","COPY",BODY,{"derivedFrom":makeQuery(id+"F2.opPattern","COPY",BODY,{"derivedFrom":makeQuery(id+"F1.opRevolve","SWEPT_BODY",BODY,{"disambiguationData":[OSD([sQuery(id+"F0.wireOp",EDGE,"E1")])]}),"instanceName":"1"}),"instanceName":"1"}),"instanceName":"1"}),"instanceName":"1"}),"instanceName":"1"}),"instanceName":"1"}),"instanceName":"1"});
            var Q1135;
            Q1135=makeQuery(id+"F12.opPattern","COPY",BODY,{"derivedFrom":makeQuery(id+"F10.opPattern","COPY",BODY,{"derivedFrom":makeQuery(id+"F9.opPattern","COPY",BODY,{"derivedFrom":makeQuery(id+"F8.opPattern","COPY",BODY,{"derivedFrom":makeQuery(id+"F7.opPattern","COPY",BODY,{"derivedFrom":makeQuery(id+"F5.opPattern","COPY",BODY,{"derivedFrom":makeQuery(id+"F3.opPattern","COPY",BODY,{"derivedFrom":makeQuery(id+"F2.opPattern","COPY",BODY,{"derivedFrom":makeQuery(id+"F1.opRevolve","SWEPT_BODY",BODY,{"disambiguationData":[OSD([sQuery(id+"F0.wireOp",EDGE,"E1")])]}),"instanceName":"1"}),"instanceName":"1"}),"instanceName":"1"}),"instanceName":"1"}),"instanceName":"1"}),"instanceName":"1"}),"instanceName":"1"}),"instanceName":"1"});
            var Q1136;
            Q1136=makeQuery(id+"F12.opPattern","COPY",BODY,{"derivedFrom":makeQuery(id+"F10.opPattern","COPY",BODY,{"derivedFrom":makeQuery(id+"F9.opPattern","COPY",BODY,{"derivedFrom":makeQuery(id+"F8.opPattern","COPY",BODY,{"derivedFrom":makeQuery(id+"F7.opPattern","COPY",BODY,{"derivedFrom":makeQuery(id+"F5.opPattern","COPY",BODY,{"derivedFrom":makeQuery(id+"F4.opPattern","COPY",BODY,{"derivedFrom":makeQuery(id+"F1.opRevolve","SWEPT_BODY",BODY,{"disambiguationData":[OSD([sQuery(id+"F0.wireOp",EDGE,"E1")])]}),"instanceName":"1"}),"instanceName":"1"}),"instanceName":"1"}),"instanceName":"1"}),"instanceName":"1"}),"instanceName":"1"}),"instanceName":"1"});
            var Q1137;
            Q1137=makeQuery(id+"F12.opPattern","COPY",BODY,{"derivedFrom":makeQuery(id+"F10.opPattern","COPY",BODY,{"derivedFrom":makeQuery(id+"F9.opPattern","COPY",BODY,{"derivedFrom":makeQuery(id+"F8.opPattern","COPY",BODY,{"derivedFrom":makeQuery(id+"F7.opPattern","COPY",BODY,{"derivedFrom":makeQuery(id+"F5.opPattern","COPY",BODY,{"derivedFrom":makeQuery(id+"F4.opPattern","COPY",BODY,{"derivedFrom":makeQuery(id+"F2.opPattern","COPY",BODY,{"derivedFrom":makeQuery(id+"F1.opRevolve","SWEPT_BODY",BODY,{"disambiguationData":[OSD([sQuery(id+"F0.wireOp",EDGE,"E1")])]}),"instanceName":"1"}),"instanceName":"1"}),"instanceName":"1"}),"instanceName":"1"}),"instanceName":"1"}),"instanceName":"1"}),"instanceName":"1"}),"instanceName":"1"});
            var Q1138;
            Q1138=makeQuery(id+"F12.opPattern","COPY",BODY,{"derivedFrom":makeQuery(id+"F10.opPattern","COPY",BODY,{"derivedFrom":makeQuery(id+"F9.opPattern","COPY",BODY,{"derivedFrom":makeQuery(id+"F8.opPattern","COPY",BODY,{"derivedFrom":makeQuery(id+"F7.opPattern","COPY",BODY,{"derivedFrom":makeQuery(id+"F5.opPattern","COPY",BODY,{"derivedFrom":makeQuery(id+"F4.opPattern","COPY",BODY,{"derivedFrom":makeQuery(id+"F3.opPattern","COPY",BODY,{"derivedFrom":makeQuery(id+"F2.opPattern","COPY",BODY,{"derivedFrom":makeQuery(id+"F1.opRevolve","SWEPT_BODY",BODY,{"disambiguationData":[OSD([sQuery(id+"F0.wireOp",EDGE,"E1")])]}),"instanceName":"1"}),"instanceName":"1"}),"instanceName":"1"}),"instanceName":"1"}),"instanceName":"1"}),"instanceName":"1"}),"instanceName":"1"}),"instanceName":"1"}),"instanceName":"1"});
            var Q1139;
            Q1139=makeQuery(id+"F12.opPattern","COPY",BODY,{"derivedFrom":makeQuery(id+"F10.opPattern","COPY",BODY,{"derivedFrom":makeQuery(id+"F9.opPattern","COPY",BODY,{"derivedFrom":makeQuery(id+"F8.opPattern","COPY",BODY,{"derivedFrom":makeQuery(id+"F7.opPattern","COPY",BODY,{"derivedFrom":makeQuery(id+"F6.opPattern","COPY",BODY,{"derivedFrom":makeQuery(id+"F1.opRevolve","SWEPT_BODY",BODY,{"disambiguationData":[OSD([sQuery(id+"F0.wireOp",EDGE,"E1")])]}),"instanceName":"1"}),"instanceName":"1"}),"instanceName":"1"}),"instanceName":"1"}),"instanceName":"1"}),"instanceName":"1"});
            var Q1140;
            Q1140=makeQuery(id+"F12.opPattern","COPY",BODY,{"derivedFrom":makeQuery(id+"F10.opPattern","COPY",BODY,{"derivedFrom":makeQuery(id+"F9.opPattern","COPY",BODY,{"derivedFrom":makeQuery(id+"F8.opPattern","COPY",BODY,{"derivedFrom":makeQuery(id+"F7.opPattern","COPY",BODY,{"derivedFrom":makeQuery(id+"F6.opPattern","COPY",BODY,{"derivedFrom":makeQuery(id+"F2.opPattern","COPY",BODY,{"derivedFrom":makeQuery(id+"F1.opRevolve","SWEPT_BODY",BODY,{"disambiguationData":[OSD([sQuery(id+"F0.wireOp",EDGE,"E1")])]}),"instanceName":"1"}),"instanceName":"1"}),"instanceName":"1"}),"instanceName":"1"}),"instanceName":"1"}),"instanceName":"1"}),"instanceName":"1"});
            var Q1141;
            Q1141=makeQuery(id+"F12.opPattern","COPY",BODY,{"derivedFrom":makeQuery(id+"F10.opPattern","COPY",BODY,{"derivedFrom":makeQuery(id+"F9.opPattern","COPY",BODY,{"derivedFrom":makeQuery(id+"F8.opPattern","COPY",BODY,{"derivedFrom":makeQuery(id+"F7.opPattern","COPY",BODY,{"derivedFrom":makeQuery(id+"F6.opPattern","COPY",BODY,{"derivedFrom":makeQuery(id+"F3.opPattern","COPY",BODY,{"derivedFrom":makeQuery(id+"F2.opPattern","COPY",BODY,{"derivedFrom":makeQuery(id+"F1.opRevolve","SWEPT_BODY",BODY,{"disambiguationData":[OSD([sQuery(id+"F0.wireOp",EDGE,"E1")])]}),"instanceName":"1"}),"instanceName":"1"}),"instanceName":"1"}),"instanceName":"1"}),"instanceName":"1"}),"instanceName":"1"}),"instanceName":"1"}),"instanceName":"1"});
            var Q1142;
            Q1142=makeQuery(id+"F12.opPattern","COPY",BODY,{"derivedFrom":makeQuery(id+"F10.opPattern","COPY",BODY,{"derivedFrom":makeQuery(id+"F9.opPattern","COPY",BODY,{"derivedFrom":makeQuery(id+"F8.opPattern","COPY",BODY,{"derivedFrom":makeQuery(id+"F7.opPattern","COPY",BODY,{"derivedFrom":makeQuery(id+"F6.opPattern","COPY",BODY,{"derivedFrom":makeQuery(id+"F4.opPattern","COPY",BODY,{"derivedFrom":makeQuery(id+"F1.opRevolve","SWEPT_BODY",BODY,{"disambiguationData":[OSD([sQuery(id+"F0.wireOp",EDGE,"E1")])]}),"instanceName":"1"}),"instanceName":"1"}),"instanceName":"1"}),"instanceName":"1"}),"instanceName":"1"}),"instanceName":"1"}),"instanceName":"1"});
            var Q1143;
            Q1143=makeQuery(id+"F12.opPattern","COPY",BODY,{"derivedFrom":makeQuery(id+"F10.opPattern","COPY",BODY,{"derivedFrom":makeQuery(id+"F9.opPattern","COPY",BODY,{"derivedFrom":makeQuery(id+"F8.opPattern","COPY",BODY,{"derivedFrom":makeQuery(id+"F7.opPattern","COPY",BODY,{"derivedFrom":makeQuery(id+"F6.opPattern","COPY",BODY,{"derivedFrom":makeQuery(id+"F4.opPattern","COPY",BODY,{"derivedFrom":makeQuery(id+"F2.opPattern","COPY",BODY,{"derivedFrom":makeQuery(id+"F1.opRevolve","SWEPT_BODY",BODY,{"disambiguationData":[OSD([sQuery(id+"F0.wireOp",EDGE,"E1")])]}),"instanceName":"1"}),"instanceName":"1"}),"instanceName":"1"}),"instanceName":"1"}),"instanceName":"1"}),"instanceName":"1"}),"instanceName":"1"}),"instanceName":"1"});
            var Q1144;
            Q1144=makeQuery(id+"F12.opPattern","COPY",BODY,{"derivedFrom":makeQuery(id+"F10.opPattern","COPY",BODY,{"derivedFrom":makeQuery(id+"F9.opPattern","COPY",BODY,{"derivedFrom":makeQuery(id+"F8.opPattern","COPY",BODY,{"derivedFrom":makeQuery(id+"F7.opPattern","COPY",BODY,{"derivedFrom":makeQuery(id+"F6.opPattern","COPY",BODY,{"derivedFrom":makeQuery(id+"F4.opPattern","COPY",BODY,{"derivedFrom":makeQuery(id+"F3.opPattern","COPY",BODY,{"derivedFrom":makeQuery(id+"F2.opPattern","COPY",BODY,{"derivedFrom":makeQuery(id+"F1.opRevolve","SWEPT_BODY",BODY,{"disambiguationData":[OSD([sQuery(id+"F0.wireOp",EDGE,"E1")])]}),"instanceName":"1"}),"instanceName":"1"}),"instanceName":"1"}),"instanceName":"1"}),"instanceName":"1"}),"instanceName":"1"}),"instanceName":"1"}),"instanceName":"1"}),"instanceName":"1"});
            var Q1145;
            Q1145=makeQuery(id+"F12.opPattern","COPY",BODY,{"derivedFrom":makeQuery(id+"F10.opPattern","COPY",BODY,{"derivedFrom":makeQuery(id+"F9.opPattern","COPY",BODY,{"derivedFrom":makeQuery(id+"F8.opPattern","COPY",BODY,{"derivedFrom":makeQuery(id+"F7.opPattern","COPY",BODY,{"derivedFrom":makeQuery(id+"F6.opPattern","COPY",BODY,{"derivedFrom":makeQuery(id+"F5.opPattern","COPY",BODY,{"derivedFrom":makeQuery(id+"F1.opRevolve","SWEPT_BODY",BODY,{"disambiguationData":[OSD([sQuery(id+"F0.wireOp",EDGE,"E1")])]}),"instanceName":"1"}),"instanceName":"1"}),"instanceName":"1"}),"instanceName":"1"}),"instanceName":"1"}),"instanceName":"1"}),"instanceName":"1"});
            var Q1146;
            Q1146=makeQuery(id+"F12.opPattern","COPY",BODY,{"derivedFrom":makeQuery(id+"F10.opPattern","COPY",BODY,{"derivedFrom":makeQuery(id+"F9.opPattern","COPY",BODY,{"derivedFrom":makeQuery(id+"F8.opPattern","COPY",BODY,{"derivedFrom":makeQuery(id+"F7.opPattern","COPY",BODY,{"derivedFrom":makeQuery(id+"F6.opPattern","COPY",BODY,{"derivedFrom":makeQuery(id+"F5.opPattern","COPY",BODY,{"derivedFrom":makeQuery(id+"F2.opPattern","COPY",BODY,{"derivedFrom":makeQuery(id+"F1.opRevolve","SWEPT_BODY",BODY,{"disambiguationData":[OSD([sQuery(id+"F0.wireOp",EDGE,"E1")])]}),"instanceName":"1"}),"instanceName":"1"}),"instanceName":"1"}),"instanceName":"1"}),"instanceName":"1"}),"instanceName":"1"}),"instanceName":"1"}),"instanceName":"1"});
            var Q1147;
            Q1147=makeQuery(id+"F12.opPattern","COPY",BODY,{"derivedFrom":makeQuery(id+"F10.opPattern","COPY",BODY,{"derivedFrom":makeQuery(id+"F9.opPattern","COPY",BODY,{"derivedFrom":makeQuery(id+"F8.opPattern","COPY",BODY,{"derivedFrom":makeQuery(id+"F7.opPattern","COPY",BODY,{"derivedFrom":makeQuery(id+"F6.opPattern","COPY",BODY,{"derivedFrom":makeQuery(id+"F5.opPattern","COPY",BODY,{"derivedFrom":makeQuery(id+"F3.opPattern","COPY",BODY,{"derivedFrom":makeQuery(id+"F2.opPattern","COPY",BODY,{"derivedFrom":makeQuery(id+"F1.opRevolve","SWEPT_BODY",BODY,{"disambiguationData":[OSD([sQuery(id+"F0.wireOp",EDGE,"E1")])]}),"instanceName":"1"}),"instanceName":"1"}),"instanceName":"1"}),"instanceName":"1"}),"instanceName":"1"}),"instanceName":"1"}),"instanceName":"1"}),"instanceName":"1"}),"instanceName":"1"});
            var Q1148;
            Q1148=makeQuery(id+"F12.opPattern","COPY",BODY,{"derivedFrom":makeQuery(id+"F10.opPattern","COPY",BODY,{"derivedFrom":makeQuery(id+"F9.opPattern","COPY",BODY,{"derivedFrom":makeQuery(id+"F8.opPattern","COPY",BODY,{"derivedFrom":makeQuery(id+"F7.opPattern","COPY",BODY,{"derivedFrom":makeQuery(id+"F6.opPattern","COPY",BODY,{"derivedFrom":makeQuery(id+"F5.opPattern","COPY",BODY,{"derivedFrom":makeQuery(id+"F4.opPattern","COPY",BODY,{"derivedFrom":makeQuery(id+"F1.opRevolve","SWEPT_BODY",BODY,{"disambiguationData":[OSD([sQuery(id+"F0.wireOp",EDGE,"E1")])]}),"instanceName":"1"}),"instanceName":"1"}),"instanceName":"1"}),"instanceName":"1"}),"instanceName":"1"}),"instanceName":"1"}),"instanceName":"1"}),"instanceName":"1"});
            var Q1149;
            Q1149=makeQuery(id+"F12.opPattern","COPY",BODY,{"derivedFrom":makeQuery(id+"F10.opPattern","COPY",BODY,{"derivedFrom":makeQuery(id+"F9.opPattern","COPY",BODY,{"derivedFrom":makeQuery(id+"F8.opPattern","COPY",BODY,{"derivedFrom":makeQuery(id+"F7.opPattern","COPY",BODY,{"derivedFrom":makeQuery(id+"F6.opPattern","COPY",BODY,{"derivedFrom":makeQuery(id+"F5.opPattern","COPY",BODY,{"derivedFrom":makeQuery(id+"F4.opPattern","COPY",BODY,{"derivedFrom":makeQuery(id+"F2.opPattern","COPY",BODY,{"derivedFrom":makeQuery(id+"F1.opRevolve","SWEPT_BODY",BODY,{"disambiguationData":[OSD([sQuery(id+"F0.wireOp",EDGE,"E1")])]}),"instanceName":"1"}),"instanceName":"1"}),"instanceName":"1"}),"instanceName":"1"}),"instanceName":"1"}),"instanceName":"1"}),"instanceName":"1"}),"instanceName":"1"}),"instanceName":"1"});
            var Q1150;
            Q1150=makeQuery(id+"F12.opPattern","COPY",BODY,{"derivedFrom":makeQuery(id+"F10.opPattern","COPY",BODY,{"derivedFrom":makeQuery(id+"F9.opPattern","COPY",BODY,{"derivedFrom":makeQuery(id+"F8.opPattern","COPY",BODY,{"derivedFrom":makeQuery(id+"F7.opPattern","COPY",BODY,{"derivedFrom":makeQuery(id+"F6.opPattern","COPY",BODY,{"derivedFrom":makeQuery(id+"F5.opPattern","COPY",BODY,{"derivedFrom":makeQuery(id+"F4.opPattern","COPY",BODY,{"derivedFrom":makeQuery(id+"F3.opPattern","COPY",BODY,{"derivedFrom":makeQuery(id+"F2.opPattern","COPY",BODY,{"derivedFrom":makeQuery(id+"F1.opRevolve","SWEPT_BODY",BODY,{"disambiguationData":[OSD([sQuery(id+"F0.wireOp",EDGE,"E1")])]}),"instanceName":"1"}),"instanceName":"1"}),"instanceName":"1"}),"instanceName":"1"}),"instanceName":"1"}),"instanceName":"1"}),"instanceName":"1"}),"instanceName":"1"}),"instanceName":"1"}),"instanceName":"1"});
            var Q1151;
            Q1151=makeQuery(id+"F12.opPattern","COPY",BODY,{"derivedFrom":makeQuery(id+"F11.opPattern","COPY",BODY,{"derivedFrom":makeQuery(id+"F1.opRevolve","SWEPT_BODY",BODY,{"disambiguationData":[OSD([sQuery(id+"F0.wireOp",EDGE,"E1")])]}),"instanceName":"1"}),"instanceName":"1"});
            var Q1152;
            Q1152=makeQuery(id+"F12.opPattern","COPY",BODY,{"derivedFrom":makeQuery(id+"F11.opPattern","COPY",BODY,{"derivedFrom":makeQuery(id+"F2.opPattern","COPY",BODY,{"derivedFrom":makeQuery(id+"F1.opRevolve","SWEPT_BODY",BODY,{"disambiguationData":[OSD([sQuery(id+"F0.wireOp",EDGE,"E1")])]}),"instanceName":"1"}),"instanceName":"1"}),"instanceName":"1"});
            var Q1153;
            Q1153=makeQuery(id+"F12.opPattern","COPY",BODY,{"derivedFrom":makeQuery(id+"F11.opPattern","COPY",BODY,{"derivedFrom":makeQuery(id+"F3.opPattern","COPY",BODY,{"derivedFrom":makeQuery(id+"F2.opPattern","COPY",BODY,{"derivedFrom":makeQuery(id+"F1.opRevolve","SWEPT_BODY",BODY,{"disambiguationData":[OSD([sQuery(id+"F0.wireOp",EDGE,"E1")])]}),"instanceName":"1"}),"instanceName":"1"}),"instanceName":"1"}),"instanceName":"1"});
            var Q1154;
            Q1154=makeQuery(id+"F12.opPattern","COPY",BODY,{"derivedFrom":makeQuery(id+"F11.opPattern","COPY",BODY,{"derivedFrom":makeQuery(id+"F4.opPattern","COPY",BODY,{"derivedFrom":makeQuery(id+"F1.opRevolve","SWEPT_BODY",BODY,{"disambiguationData":[OSD([sQuery(id+"F0.wireOp",EDGE,"E1")])]}),"instanceName":"1"}),"instanceName":"1"}),"instanceName":"1"});
            var Q1155;
            Q1155=makeQuery(id+"F12.opPattern","COPY",BODY,{"derivedFrom":makeQuery(id+"F11.opPattern","COPY",BODY,{"derivedFrom":makeQuery(id+"F4.opPattern","COPY",BODY,{"derivedFrom":makeQuery(id+"F2.opPattern","COPY",BODY,{"derivedFrom":makeQuery(id+"F1.opRevolve","SWEPT_BODY",BODY,{"disambiguationData":[OSD([sQuery(id+"F0.wireOp",EDGE,"E1")])]}),"instanceName":"1"}),"instanceName":"1"}),"instanceName":"1"}),"instanceName":"1"});
            var Q1156;
            Q1156=makeQuery(id+"F12.opPattern","COPY",BODY,{"derivedFrom":makeQuery(id+"F11.opPattern","COPY",BODY,{"derivedFrom":makeQuery(id+"F4.opPattern","COPY",BODY,{"derivedFrom":makeQuery(id+"F3.opPattern","COPY",BODY,{"derivedFrom":makeQuery(id+"F2.opPattern","COPY",BODY,{"derivedFrom":makeQuery(id+"F1.opRevolve","SWEPT_BODY",BODY,{"disambiguationData":[OSD([sQuery(id+"F0.wireOp",EDGE,"E1")])]}),"instanceName":"1"}),"instanceName":"1"}),"instanceName":"1"}),"instanceName":"1"}),"instanceName":"1"});
            var Q1157;
            Q1157=makeQuery(id+"F12.opPattern","COPY",BODY,{"derivedFrom":makeQuery(id+"F11.opPattern","COPY",BODY,{"derivedFrom":makeQuery(id+"F5.opPattern","COPY",BODY,{"derivedFrom":makeQuery(id+"F1.opRevolve","SWEPT_BODY",BODY,{"disambiguationData":[OSD([sQuery(id+"F0.wireOp",EDGE,"E1")])]}),"instanceName":"1"}),"instanceName":"1"}),"instanceName":"1"});
            var Q1158;
            Q1158=makeQuery(id+"F12.opPattern","COPY",BODY,{"derivedFrom":makeQuery(id+"F11.opPattern","COPY",BODY,{"derivedFrom":makeQuery(id+"F5.opPattern","COPY",BODY,{"derivedFrom":makeQuery(id+"F2.opPattern","COPY",BODY,{"derivedFrom":makeQuery(id+"F1.opRevolve","SWEPT_BODY",BODY,{"disambiguationData":[OSD([sQuery(id+"F0.wireOp",EDGE,"E1")])]}),"instanceName":"1"}),"instanceName":"1"}),"instanceName":"1"}),"instanceName":"1"});
            var Q1159;
            Q1159=makeQuery(id+"F12.opPattern","COPY",BODY,{"derivedFrom":makeQuery(id+"F11.opPattern","COPY",BODY,{"derivedFrom":makeQuery(id+"F5.opPattern","COPY",BODY,{"derivedFrom":makeQuery(id+"F3.opPattern","COPY",BODY,{"derivedFrom":makeQuery(id+"F2.opPattern","COPY",BODY,{"derivedFrom":makeQuery(id+"F1.opRevolve","SWEPT_BODY",BODY,{"disambiguationData":[OSD([sQuery(id+"F0.wireOp",EDGE,"E1")])]}),"instanceName":"1"}),"instanceName":"1"}),"instanceName":"1"}),"instanceName":"1"}),"instanceName":"1"});
            var Q1160;
            Q1160=makeQuery(id+"F12.opPattern","COPY",BODY,{"derivedFrom":makeQuery(id+"F11.opPattern","COPY",BODY,{"derivedFrom":makeQuery(id+"F5.opPattern","COPY",BODY,{"derivedFrom":makeQuery(id+"F4.opPattern","COPY",BODY,{"derivedFrom":makeQuery(id+"F1.opRevolve","SWEPT_BODY",BODY,{"disambiguationData":[OSD([sQuery(id+"F0.wireOp",EDGE,"E1")])]}),"instanceName":"1"}),"instanceName":"1"}),"instanceName":"1"}),"instanceName":"1"});
            var Q1161;
            Q1161=makeQuery(id+"F12.opPattern","COPY",BODY,{"derivedFrom":makeQuery(id+"F11.opPattern","COPY",BODY,{"derivedFrom":makeQuery(id+"F5.opPattern","COPY",BODY,{"derivedFrom":makeQuery(id+"F4.opPattern","COPY",BODY,{"derivedFrom":makeQuery(id+"F2.opPattern","COPY",BODY,{"derivedFrom":makeQuery(id+"F1.opRevolve","SWEPT_BODY",BODY,{"disambiguationData":[OSD([sQuery(id+"F0.wireOp",EDGE,"E1")])]}),"instanceName":"1"}),"instanceName":"1"}),"instanceName":"1"}),"instanceName":"1"}),"instanceName":"1"});
            var Q1162;
            Q1162=makeQuery(id+"F12.opPattern","COPY",BODY,{"derivedFrom":makeQuery(id+"F11.opPattern","COPY",BODY,{"derivedFrom":makeQuery(id+"F5.opPattern","COPY",BODY,{"derivedFrom":makeQuery(id+"F4.opPattern","COPY",BODY,{"derivedFrom":makeQuery(id+"F3.opPattern","COPY",BODY,{"derivedFrom":makeQuery(id+"F2.opPattern","COPY",BODY,{"derivedFrom":makeQuery(id+"F1.opRevolve","SWEPT_BODY",BODY,{"disambiguationData":[OSD([sQuery(id+"F0.wireOp",EDGE,"E1")])]}),"instanceName":"1"}),"instanceName":"1"}),"instanceName":"1"}),"instanceName":"1"}),"instanceName":"1"}),"instanceName":"1"});
            var Q1163;
            Q1163=makeQuery(id+"F12.opPattern","COPY",BODY,{"derivedFrom":makeQuery(id+"F11.opPattern","COPY",BODY,{"derivedFrom":makeQuery(id+"F6.opPattern","COPY",BODY,{"derivedFrom":makeQuery(id+"F1.opRevolve","SWEPT_BODY",BODY,{"disambiguationData":[OSD([sQuery(id+"F0.wireOp",EDGE,"E1")])]}),"instanceName":"1"}),"instanceName":"1"}),"instanceName":"1"});
            var Q1164;
            Q1164=makeQuery(id+"F12.opPattern","COPY",BODY,{"derivedFrom":makeQuery(id+"F11.opPattern","COPY",BODY,{"derivedFrom":makeQuery(id+"F6.opPattern","COPY",BODY,{"derivedFrom":makeQuery(id+"F2.opPattern","COPY",BODY,{"derivedFrom":makeQuery(id+"F1.opRevolve","SWEPT_BODY",BODY,{"disambiguationData":[OSD([sQuery(id+"F0.wireOp",EDGE,"E1")])]}),"instanceName":"1"}),"instanceName":"1"}),"instanceName":"1"}),"instanceName":"1"});
            var Q1165;
            Q1165=makeQuery(id+"F12.opPattern","COPY",BODY,{"derivedFrom":makeQuery(id+"F11.opPattern","COPY",BODY,{"derivedFrom":makeQuery(id+"F6.opPattern","COPY",BODY,{"derivedFrom":makeQuery(id+"F3.opPattern","COPY",BODY,{"derivedFrom":makeQuery(id+"F2.opPattern","COPY",BODY,{"derivedFrom":makeQuery(id+"F1.opRevolve","SWEPT_BODY",BODY,{"disambiguationData":[OSD([sQuery(id+"F0.wireOp",EDGE,"E1")])]}),"instanceName":"1"}),"instanceName":"1"}),"instanceName":"1"}),"instanceName":"1"}),"instanceName":"1"});
            var Q1166;
            Q1166=makeQuery(id+"F12.opPattern","COPY",BODY,{"derivedFrom":makeQuery(id+"F11.opPattern","COPY",BODY,{"derivedFrom":makeQuery(id+"F6.opPattern","COPY",BODY,{"derivedFrom":makeQuery(id+"F4.opPattern","COPY",BODY,{"derivedFrom":makeQuery(id+"F1.opRevolve","SWEPT_BODY",BODY,{"disambiguationData":[OSD([sQuery(id+"F0.wireOp",EDGE,"E1")])]}),"instanceName":"1"}),"instanceName":"1"}),"instanceName":"1"}),"instanceName":"1"});
            var Q1167;
            Q1167=makeQuery(id+"F12.opPattern","COPY",BODY,{"derivedFrom":makeQuery(id+"F11.opPattern","COPY",BODY,{"derivedFrom":makeQuery(id+"F6.opPattern","COPY",BODY,{"derivedFrom":makeQuery(id+"F4.opPattern","COPY",BODY,{"derivedFrom":makeQuery(id+"F2.opPattern","COPY",BODY,{"derivedFrom":makeQuery(id+"F1.opRevolve","SWEPT_BODY",BODY,{"disambiguationData":[OSD([sQuery(id+"F0.wireOp",EDGE,"E1")])]}),"instanceName":"1"}),"instanceName":"1"}),"instanceName":"1"}),"instanceName":"1"}),"instanceName":"1"});
            var Q1168;
            Q1168=makeQuery(id+"F12.opPattern","COPY",BODY,{"derivedFrom":makeQuery(id+"F11.opPattern","COPY",BODY,{"derivedFrom":makeQuery(id+"F6.opPattern","COPY",BODY,{"derivedFrom":makeQuery(id+"F4.opPattern","COPY",BODY,{"derivedFrom":makeQuery(id+"F3.opPattern","COPY",BODY,{"derivedFrom":makeQuery(id+"F2.opPattern","COPY",BODY,{"derivedFrom":makeQuery(id+"F1.opRevolve","SWEPT_BODY",BODY,{"disambiguationData":[OSD([sQuery(id+"F0.wireOp",EDGE,"E1")])]}),"instanceName":"1"}),"instanceName":"1"}),"instanceName":"1"}),"instanceName":"1"}),"instanceName":"1"}),"instanceName":"1"});
            var Q1169;
            Q1169=makeQuery(id+"F12.opPattern","COPY",BODY,{"derivedFrom":makeQuery(id+"F11.opPattern","COPY",BODY,{"derivedFrom":makeQuery(id+"F6.opPattern","COPY",BODY,{"derivedFrom":makeQuery(id+"F5.opPattern","COPY",BODY,{"derivedFrom":makeQuery(id+"F1.opRevolve","SWEPT_BODY",BODY,{"disambiguationData":[OSD([sQuery(id+"F0.wireOp",EDGE,"E1")])]}),"instanceName":"1"}),"instanceName":"1"}),"instanceName":"1"}),"instanceName":"1"});
            var Q1170;
            Q1170=makeQuery(id+"F12.opPattern","COPY",BODY,{"derivedFrom":makeQuery(id+"F11.opPattern","COPY",BODY,{"derivedFrom":makeQuery(id+"F6.opPattern","COPY",BODY,{"derivedFrom":makeQuery(id+"F5.opPattern","COPY",BODY,{"derivedFrom":makeQuery(id+"F2.opPattern","COPY",BODY,{"derivedFrom":makeQuery(id+"F1.opRevolve","SWEPT_BODY",BODY,{"disambiguationData":[OSD([sQuery(id+"F0.wireOp",EDGE,"E1")])]}),"instanceName":"1"}),"instanceName":"1"}),"instanceName":"1"}),"instanceName":"1"}),"instanceName":"1"});
            var Q1171;
            Q1171=makeQuery(id+"F12.opPattern","COPY",BODY,{"derivedFrom":makeQuery(id+"F11.opPattern","COPY",BODY,{"derivedFrom":makeQuery(id+"F6.opPattern","COPY",BODY,{"derivedFrom":makeQuery(id+"F5.opPattern","COPY",BODY,{"derivedFrom":makeQuery(id+"F3.opPattern","COPY",BODY,{"derivedFrom":makeQuery(id+"F2.opPattern","COPY",BODY,{"derivedFrom":makeQuery(id+"F1.opRevolve","SWEPT_BODY",BODY,{"disambiguationData":[OSD([sQuery(id+"F0.wireOp",EDGE,"E1")])]}),"instanceName":"1"}),"instanceName":"1"}),"instanceName":"1"}),"instanceName":"1"}),"instanceName":"1"}),"instanceName":"1"});
            var Q1172;
            Q1172=makeQuery(id+"F12.opPattern","COPY",BODY,{"derivedFrom":makeQuery(id+"F11.opPattern","COPY",BODY,{"derivedFrom":makeQuery(id+"F6.opPattern","COPY",BODY,{"derivedFrom":makeQuery(id+"F5.opPattern","COPY",BODY,{"derivedFrom":makeQuery(id+"F4.opPattern","COPY",BODY,{"derivedFrom":makeQuery(id+"F1.opRevolve","SWEPT_BODY",BODY,{"disambiguationData":[OSD([sQuery(id+"F0.wireOp",EDGE,"E1")])]}),"instanceName":"1"}),"instanceName":"1"}),"instanceName":"1"}),"instanceName":"1"}),"instanceName":"1"});
            var Q1173;
            Q1173=makeQuery(id+"F12.opPattern","COPY",BODY,{"derivedFrom":makeQuery(id+"F11.opPattern","COPY",BODY,{"derivedFrom":makeQuery(id+"F6.opPattern","COPY",BODY,{"derivedFrom":makeQuery(id+"F5.opPattern","COPY",BODY,{"derivedFrom":makeQuery(id+"F4.opPattern","COPY",BODY,{"derivedFrom":makeQuery(id+"F2.opPattern","COPY",BODY,{"derivedFrom":makeQuery(id+"F1.opRevolve","SWEPT_BODY",BODY,{"disambiguationData":[OSD([sQuery(id+"F0.wireOp",EDGE,"E1")])]}),"instanceName":"1"}),"instanceName":"1"}),"instanceName":"1"}),"instanceName":"1"}),"instanceName":"1"}),"instanceName":"1"});
            var Q1174;
            Q1174=makeQuery(id+"F12.opPattern","COPY",BODY,{"derivedFrom":makeQuery(id+"F11.opPattern","COPY",BODY,{"derivedFrom":makeQuery(id+"F6.opPattern","COPY",BODY,{"derivedFrom":makeQuery(id+"F5.opPattern","COPY",BODY,{"derivedFrom":makeQuery(id+"F4.opPattern","COPY",BODY,{"derivedFrom":makeQuery(id+"F3.opPattern","COPY",BODY,{"derivedFrom":makeQuery(id+"F2.opPattern","COPY",BODY,{"derivedFrom":makeQuery(id+"F1.opRevolve","SWEPT_BODY",BODY,{"disambiguationData":[OSD([sQuery(id+"F0.wireOp",EDGE,"E1")])]}),"instanceName":"1"}),"instanceName":"1"}),"instanceName":"1"}),"instanceName":"1"}),"instanceName":"1"}),"instanceName":"1"}),"instanceName":"1"});
            var Q1175;
            Q1175=makeQuery(id+"F12.opPattern","COPY",BODY,{"derivedFrom":makeQuery(id+"F11.opPattern","COPY",BODY,{"derivedFrom":makeQuery(id+"F7.opPattern","COPY",BODY,{"derivedFrom":makeQuery(id+"F1.opRevolve","SWEPT_BODY",BODY,{"disambiguationData":[OSD([sQuery(id+"F0.wireOp",EDGE,"E1")])]}),"instanceName":"1"}),"instanceName":"1"}),"instanceName":"1"});
            var Q1176;
            Q1176=makeQuery(id+"F12.opPattern","COPY",BODY,{"derivedFrom":makeQuery(id+"F11.opPattern","COPY",BODY,{"derivedFrom":makeQuery(id+"F7.opPattern","COPY",BODY,{"derivedFrom":makeQuery(id+"F2.opPattern","COPY",BODY,{"derivedFrom":makeQuery(id+"F1.opRevolve","SWEPT_BODY",BODY,{"disambiguationData":[OSD([sQuery(id+"F0.wireOp",EDGE,"E1")])]}),"instanceName":"1"}),"instanceName":"1"}),"instanceName":"1"}),"instanceName":"1"});
            var Q1177;
            Q1177=makeQuery(id+"F12.opPattern","COPY",BODY,{"derivedFrom":makeQuery(id+"F11.opPattern","COPY",BODY,{"derivedFrom":makeQuery(id+"F7.opPattern","COPY",BODY,{"derivedFrom":makeQuery(id+"F3.opPattern","COPY",BODY,{"derivedFrom":makeQuery(id+"F2.opPattern","COPY",BODY,{"derivedFrom":makeQuery(id+"F1.opRevolve","SWEPT_BODY",BODY,{"disambiguationData":[OSD([sQuery(id+"F0.wireOp",EDGE,"E1")])]}),"instanceName":"1"}),"instanceName":"1"}),"instanceName":"1"}),"instanceName":"1"}),"instanceName":"1"});
            var Q1178;
            Q1178=makeQuery(id+"F12.opPattern","COPY",BODY,{"derivedFrom":makeQuery(id+"F11.opPattern","COPY",BODY,{"derivedFrom":makeQuery(id+"F7.opPattern","COPY",BODY,{"derivedFrom":makeQuery(id+"F4.opPattern","COPY",BODY,{"derivedFrom":makeQuery(id+"F1.opRevolve","SWEPT_BODY",BODY,{"disambiguationData":[OSD([sQuery(id+"F0.wireOp",EDGE,"E1")])]}),"instanceName":"1"}),"instanceName":"1"}),"instanceName":"1"}),"instanceName":"1"});
            var Q1179;
            Q1179=makeQuery(id+"F12.opPattern","COPY",BODY,{"derivedFrom":makeQuery(id+"F11.opPattern","COPY",BODY,{"derivedFrom":makeQuery(id+"F7.opPattern","COPY",BODY,{"derivedFrom":makeQuery(id+"F4.opPattern","COPY",BODY,{"derivedFrom":makeQuery(id+"F2.opPattern","COPY",BODY,{"derivedFrom":makeQuery(id+"F1.opRevolve","SWEPT_BODY",BODY,{"disambiguationData":[OSD([sQuery(id+"F0.wireOp",EDGE,"E1")])]}),"instanceName":"1"}),"instanceName":"1"}),"instanceName":"1"}),"instanceName":"1"}),"instanceName":"1"});
            var Q1180;
            Q1180=makeQuery(id+"F12.opPattern","COPY",BODY,{"derivedFrom":makeQuery(id+"F11.opPattern","COPY",BODY,{"derivedFrom":makeQuery(id+"F7.opPattern","COPY",BODY,{"derivedFrom":makeQuery(id+"F4.opPattern","COPY",BODY,{"derivedFrom":makeQuery(id+"F3.opPattern","COPY",BODY,{"derivedFrom":makeQuery(id+"F2.opPattern","COPY",BODY,{"derivedFrom":makeQuery(id+"F1.opRevolve","SWEPT_BODY",BODY,{"disambiguationData":[OSD([sQuery(id+"F0.wireOp",EDGE,"E1")])]}),"instanceName":"1"}),"instanceName":"1"}),"instanceName":"1"}),"instanceName":"1"}),"instanceName":"1"}),"instanceName":"1"});
            var Q1181;
            Q1181=makeQuery(id+"F12.opPattern","COPY",BODY,{"derivedFrom":makeQuery(id+"F11.opPattern","COPY",BODY,{"derivedFrom":makeQuery(id+"F7.opPattern","COPY",BODY,{"derivedFrom":makeQuery(id+"F5.opPattern","COPY",BODY,{"derivedFrom":makeQuery(id+"F1.opRevolve","SWEPT_BODY",BODY,{"disambiguationData":[OSD([sQuery(id+"F0.wireOp",EDGE,"E1")])]}),"instanceName":"1"}),"instanceName":"1"}),"instanceName":"1"}),"instanceName":"1"});
            var Q1182;
            Q1182=makeQuery(id+"F12.opPattern","COPY",BODY,{"derivedFrom":makeQuery(id+"F11.opPattern","COPY",BODY,{"derivedFrom":makeQuery(id+"F7.opPattern","COPY",BODY,{"derivedFrom":makeQuery(id+"F5.opPattern","COPY",BODY,{"derivedFrom":makeQuery(id+"F2.opPattern","COPY",BODY,{"derivedFrom":makeQuery(id+"F1.opRevolve","SWEPT_BODY",BODY,{"disambiguationData":[OSD([sQuery(id+"F0.wireOp",EDGE,"E1")])]}),"instanceName":"1"}),"instanceName":"1"}),"instanceName":"1"}),"instanceName":"1"}),"instanceName":"1"});
            var Q1183;
            Q1183=makeQuery(id+"F12.opPattern","COPY",BODY,{"derivedFrom":makeQuery(id+"F11.opPattern","COPY",BODY,{"derivedFrom":makeQuery(id+"F7.opPattern","COPY",BODY,{"derivedFrom":makeQuery(id+"F5.opPattern","COPY",BODY,{"derivedFrom":makeQuery(id+"F3.opPattern","COPY",BODY,{"derivedFrom":makeQuery(id+"F2.opPattern","COPY",BODY,{"derivedFrom":makeQuery(id+"F1.opRevolve","SWEPT_BODY",BODY,{"disambiguationData":[OSD([sQuery(id+"F0.wireOp",EDGE,"E1")])]}),"instanceName":"1"}),"instanceName":"1"}),"instanceName":"1"}),"instanceName":"1"}),"instanceName":"1"}),"instanceName":"1"});
            var Q1184;
            Q1184=makeQuery(id+"F12.opPattern","COPY",BODY,{"derivedFrom":makeQuery(id+"F11.opPattern","COPY",BODY,{"derivedFrom":makeQuery(id+"F7.opPattern","COPY",BODY,{"derivedFrom":makeQuery(id+"F5.opPattern","COPY",BODY,{"derivedFrom":makeQuery(id+"F4.opPattern","COPY",BODY,{"derivedFrom":makeQuery(id+"F1.opRevolve","SWEPT_BODY",BODY,{"disambiguationData":[OSD([sQuery(id+"F0.wireOp",EDGE,"E1")])]}),"instanceName":"1"}),"instanceName":"1"}),"instanceName":"1"}),"instanceName":"1"}),"instanceName":"1"});
            var Q1185;
            Q1185=makeQuery(id+"F12.opPattern","COPY",BODY,{"derivedFrom":makeQuery(id+"F11.opPattern","COPY",BODY,{"derivedFrom":makeQuery(id+"F7.opPattern","COPY",BODY,{"derivedFrom":makeQuery(id+"F5.opPattern","COPY",BODY,{"derivedFrom":makeQuery(id+"F4.opPattern","COPY",BODY,{"derivedFrom":makeQuery(id+"F2.opPattern","COPY",BODY,{"derivedFrom":makeQuery(id+"F1.opRevolve","SWEPT_BODY",BODY,{"disambiguationData":[OSD([sQuery(id+"F0.wireOp",EDGE,"E1")])]}),"instanceName":"1"}),"instanceName":"1"}),"instanceName":"1"}),"instanceName":"1"}),"instanceName":"1"}),"instanceName":"1"});
            var Q1186;
            Q1186=makeQuery(id+"F12.opPattern","COPY",BODY,{"derivedFrom":makeQuery(id+"F11.opPattern","COPY",BODY,{"derivedFrom":makeQuery(id+"F7.opPattern","COPY",BODY,{"derivedFrom":makeQuery(id+"F5.opPattern","COPY",BODY,{"derivedFrom":makeQuery(id+"F4.opPattern","COPY",BODY,{"derivedFrom":makeQuery(id+"F3.opPattern","COPY",BODY,{"derivedFrom":makeQuery(id+"F2.opPattern","COPY",BODY,{"derivedFrom":makeQuery(id+"F1.opRevolve","SWEPT_BODY",BODY,{"disambiguationData":[OSD([sQuery(id+"F0.wireOp",EDGE,"E1")])]}),"instanceName":"1"}),"instanceName":"1"}),"instanceName":"1"}),"instanceName":"1"}),"instanceName":"1"}),"instanceName":"1"}),"instanceName":"1"});
            var Q1187;
            Q1187=makeQuery(id+"F12.opPattern","COPY",BODY,{"derivedFrom":makeQuery(id+"F11.opPattern","COPY",BODY,{"derivedFrom":makeQuery(id+"F7.opPattern","COPY",BODY,{"derivedFrom":makeQuery(id+"F6.opPattern","COPY",BODY,{"derivedFrom":makeQuery(id+"F1.opRevolve","SWEPT_BODY",BODY,{"disambiguationData":[OSD([sQuery(id+"F0.wireOp",EDGE,"E1")])]}),"instanceName":"1"}),"instanceName":"1"}),"instanceName":"1"}),"instanceName":"1"});
            var Q1188;
            Q1188=makeQuery(id+"F12.opPattern","COPY",BODY,{"derivedFrom":makeQuery(id+"F11.opPattern","COPY",BODY,{"derivedFrom":makeQuery(id+"F7.opPattern","COPY",BODY,{"derivedFrom":makeQuery(id+"F6.opPattern","COPY",BODY,{"derivedFrom":makeQuery(id+"F2.opPattern","COPY",BODY,{"derivedFrom":makeQuery(id+"F1.opRevolve","SWEPT_BODY",BODY,{"disambiguationData":[OSD([sQuery(id+"F0.wireOp",EDGE,"E1")])]}),"instanceName":"1"}),"instanceName":"1"}),"instanceName":"1"}),"instanceName":"1"}),"instanceName":"1"});
            var Q1189;
            Q1189=makeQuery(id+"F12.opPattern","COPY",BODY,{"derivedFrom":makeQuery(id+"F11.opPattern","COPY",BODY,{"derivedFrom":makeQuery(id+"F7.opPattern","COPY",BODY,{"derivedFrom":makeQuery(id+"F6.opPattern","COPY",BODY,{"derivedFrom":makeQuery(id+"F3.opPattern","COPY",BODY,{"derivedFrom":makeQuery(id+"F2.opPattern","COPY",BODY,{"derivedFrom":makeQuery(id+"F1.opRevolve","SWEPT_BODY",BODY,{"disambiguationData":[OSD([sQuery(id+"F0.wireOp",EDGE,"E1")])]}),"instanceName":"1"}),"instanceName":"1"}),"instanceName":"1"}),"instanceName":"1"}),"instanceName":"1"}),"instanceName":"1"});
            var Q1190;
            Q1190=makeQuery(id+"F12.opPattern","COPY",BODY,{"derivedFrom":makeQuery(id+"F11.opPattern","COPY",BODY,{"derivedFrom":makeQuery(id+"F7.opPattern","COPY",BODY,{"derivedFrom":makeQuery(id+"F6.opPattern","COPY",BODY,{"derivedFrom":makeQuery(id+"F4.opPattern","COPY",BODY,{"derivedFrom":makeQuery(id+"F1.opRevolve","SWEPT_BODY",BODY,{"disambiguationData":[OSD([sQuery(id+"F0.wireOp",EDGE,"E1")])]}),"instanceName":"1"}),"instanceName":"1"}),"instanceName":"1"}),"instanceName":"1"}),"instanceName":"1"});
            var Q1191;
            Q1191=makeQuery(id+"F12.opPattern","COPY",BODY,{"derivedFrom":makeQuery(id+"F11.opPattern","COPY",BODY,{"derivedFrom":makeQuery(id+"F7.opPattern","COPY",BODY,{"derivedFrom":makeQuery(id+"F6.opPattern","COPY",BODY,{"derivedFrom":makeQuery(id+"F4.opPattern","COPY",BODY,{"derivedFrom":makeQuery(id+"F2.opPattern","COPY",BODY,{"derivedFrom":makeQuery(id+"F1.opRevolve","SWEPT_BODY",BODY,{"disambiguationData":[OSD([sQuery(id+"F0.wireOp",EDGE,"E1")])]}),"instanceName":"1"}),"instanceName":"1"}),"instanceName":"1"}),"instanceName":"1"}),"instanceName":"1"}),"instanceName":"1"});
            var Q1192;
            Q1192=makeQuery(id+"F12.opPattern","COPY",BODY,{"derivedFrom":makeQuery(id+"F11.opPattern","COPY",BODY,{"derivedFrom":makeQuery(id+"F7.opPattern","COPY",BODY,{"derivedFrom":makeQuery(id+"F6.opPattern","COPY",BODY,{"derivedFrom":makeQuery(id+"F4.opPattern","COPY",BODY,{"derivedFrom":makeQuery(id+"F3.opPattern","COPY",BODY,{"derivedFrom":makeQuery(id+"F2.opPattern","COPY",BODY,{"derivedFrom":makeQuery(id+"F1.opRevolve","SWEPT_BODY",BODY,{"disambiguationData":[OSD([sQuery(id+"F0.wireOp",EDGE,"E1")])]}),"instanceName":"1"}),"instanceName":"1"}),"instanceName":"1"}),"instanceName":"1"}),"instanceName":"1"}),"instanceName":"1"}),"instanceName":"1"});
            var Q1193;
            Q1193=makeQuery(id+"F12.opPattern","COPY",BODY,{"derivedFrom":makeQuery(id+"F11.opPattern","COPY",BODY,{"derivedFrom":makeQuery(id+"F7.opPattern","COPY",BODY,{"derivedFrom":makeQuery(id+"F6.opPattern","COPY",BODY,{"derivedFrom":makeQuery(id+"F5.opPattern","COPY",BODY,{"derivedFrom":makeQuery(id+"F1.opRevolve","SWEPT_BODY",BODY,{"disambiguationData":[OSD([sQuery(id+"F0.wireOp",EDGE,"E1")])]}),"instanceName":"1"}),"instanceName":"1"}),"instanceName":"1"}),"instanceName":"1"}),"instanceName":"1"});
            var Q1194;
            Q1194=makeQuery(id+"F12.opPattern","COPY",BODY,{"derivedFrom":makeQuery(id+"F11.opPattern","COPY",BODY,{"derivedFrom":makeQuery(id+"F7.opPattern","COPY",BODY,{"derivedFrom":makeQuery(id+"F6.opPattern","COPY",BODY,{"derivedFrom":makeQuery(id+"F5.opPattern","COPY",BODY,{"derivedFrom":makeQuery(id+"F2.opPattern","COPY",BODY,{"derivedFrom":makeQuery(id+"F1.opRevolve","SWEPT_BODY",BODY,{"disambiguationData":[OSD([sQuery(id+"F0.wireOp",EDGE,"E1")])]}),"instanceName":"1"}),"instanceName":"1"}),"instanceName":"1"}),"instanceName":"1"}),"instanceName":"1"}),"instanceName":"1"});
            var Q1195;
            Q1195=makeQuery(id+"F12.opPattern","COPY",BODY,{"derivedFrom":makeQuery(id+"F11.opPattern","COPY",BODY,{"derivedFrom":makeQuery(id+"F7.opPattern","COPY",BODY,{"derivedFrom":makeQuery(id+"F6.opPattern","COPY",BODY,{"derivedFrom":makeQuery(id+"F5.opPattern","COPY",BODY,{"derivedFrom":makeQuery(id+"F3.opPattern","COPY",BODY,{"derivedFrom":makeQuery(id+"F2.opPattern","COPY",BODY,{"derivedFrom":makeQuery(id+"F1.opRevolve","SWEPT_BODY",BODY,{"disambiguationData":[OSD([sQuery(id+"F0.wireOp",EDGE,"E1")])]}),"instanceName":"1"}),"instanceName":"1"}),"instanceName":"1"}),"instanceName":"1"}),"instanceName":"1"}),"instanceName":"1"}),"instanceName":"1"});
            var Q1196;
            Q1196=makeQuery(id+"F12.opPattern","COPY",BODY,{"derivedFrom":makeQuery(id+"F11.opPattern","COPY",BODY,{"derivedFrom":makeQuery(id+"F7.opPattern","COPY",BODY,{"derivedFrom":makeQuery(id+"F6.opPattern","COPY",BODY,{"derivedFrom":makeQuery(id+"F5.opPattern","COPY",BODY,{"derivedFrom":makeQuery(id+"F4.opPattern","COPY",BODY,{"derivedFrom":makeQuery(id+"F1.opRevolve","SWEPT_BODY",BODY,{"disambiguationData":[OSD([sQuery(id+"F0.wireOp",EDGE,"E1")])]}),"instanceName":"1"}),"instanceName":"1"}),"instanceName":"1"}),"instanceName":"1"}),"instanceName":"1"}),"instanceName":"1"});
            var Q1197;
            Q1197=makeQuery(id+"F12.opPattern","COPY",BODY,{"derivedFrom":makeQuery(id+"F11.opPattern","COPY",BODY,{"derivedFrom":makeQuery(id+"F7.opPattern","COPY",BODY,{"derivedFrom":makeQuery(id+"F6.opPattern","COPY",BODY,{"derivedFrom":makeQuery(id+"F5.opPattern","COPY",BODY,{"derivedFrom":makeQuery(id+"F4.opPattern","COPY",BODY,{"derivedFrom":makeQuery(id+"F2.opPattern","COPY",BODY,{"derivedFrom":makeQuery(id+"F1.opRevolve","SWEPT_BODY",BODY,{"disambiguationData":[OSD([sQuery(id+"F0.wireOp",EDGE,"E1")])]}),"instanceName":"1"}),"instanceName":"1"}),"instanceName":"1"}),"instanceName":"1"}),"instanceName":"1"}),"instanceName":"1"}),"instanceName":"1"});
            var Q1198;
            Q1198=makeQuery(id+"F12.opPattern","COPY",BODY,{"derivedFrom":makeQuery(id+"F11.opPattern","COPY",BODY,{"derivedFrom":makeQuery(id+"F7.opPattern","COPY",BODY,{"derivedFrom":makeQuery(id+"F6.opPattern","COPY",BODY,{"derivedFrom":makeQuery(id+"F5.opPattern","COPY",BODY,{"derivedFrom":makeQuery(id+"F4.opPattern","COPY",BODY,{"derivedFrom":makeQuery(id+"F3.opPattern","COPY",BODY,{"derivedFrom":makeQuery(id+"F2.opPattern","COPY",BODY,{"derivedFrom":makeQuery(id+"F1.opRevolve","SWEPT_BODY",BODY,{"disambiguationData":[OSD([sQuery(id+"F0.wireOp",EDGE,"E1")])]}),"instanceName":"1"}),"instanceName":"1"}),"instanceName":"1"}),"instanceName":"1"}),"instanceName":"1"}),"instanceName":"1"}),"instanceName":"1"}),"instanceName":"1"});
            var Q1199;
            Q1199=makeQuery(id+"F12.opPattern","COPY",BODY,{"derivedFrom":makeQuery(id+"F11.opPattern","COPY",BODY,{"derivedFrom":makeQuery(id+"F8.opPattern","COPY",BODY,{"derivedFrom":makeQuery(id+"F1.opRevolve","SWEPT_BODY",BODY,{"disambiguationData":[OSD([sQuery(id+"F0.wireOp",EDGE,"E1")])]}),"instanceName":"1"}),"instanceName":"1"}),"instanceName":"1"});
            var Q1200;
            Q1200=makeQuery(id+"F12.opPattern","COPY",BODY,{"derivedFrom":makeQuery(id+"F11.opPattern","COPY",BODY,{"derivedFrom":makeQuery(id+"F8.opPattern","COPY",BODY,{"derivedFrom":makeQuery(id+"F2.opPattern","COPY",BODY,{"derivedFrom":makeQuery(id+"F1.opRevolve","SWEPT_BODY",BODY,{"disambiguationData":[OSD([sQuery(id+"F0.wireOp",EDGE,"E1")])]}),"instanceName":"1"}),"instanceName":"1"}),"instanceName":"1"}),"instanceName":"1"});
            var Q1201;
            Q1201=makeQuery(id+"F12.opPattern","COPY",BODY,{"derivedFrom":makeQuery(id+"F11.opPattern","COPY",BODY,{"derivedFrom":makeQuery(id+"F8.opPattern","COPY",BODY,{"derivedFrom":makeQuery(id+"F3.opPattern","COPY",BODY,{"derivedFrom":makeQuery(id+"F2.opPattern","COPY",BODY,{"derivedFrom":makeQuery(id+"F1.opRevolve","SWEPT_BODY",BODY,{"disambiguationData":[OSD([sQuery(id+"F0.wireOp",EDGE,"E1")])]}),"instanceName":"1"}),"instanceName":"1"}),"instanceName":"1"}),"instanceName":"1"}),"instanceName":"1"});
            var Q1202;
            Q1202=makeQuery(id+"F12.opPattern","COPY",BODY,{"derivedFrom":makeQuery(id+"F11.opPattern","COPY",BODY,{"derivedFrom":makeQuery(id+"F8.opPattern","COPY",BODY,{"derivedFrom":makeQuery(id+"F4.opPattern","COPY",BODY,{"derivedFrom":makeQuery(id+"F1.opRevolve","SWEPT_BODY",BODY,{"disambiguationData":[OSD([sQuery(id+"F0.wireOp",EDGE,"E1")])]}),"instanceName":"1"}),"instanceName":"1"}),"instanceName":"1"}),"instanceName":"1"});
            var Q1203;
            Q1203=makeQuery(id+"F12.opPattern","COPY",BODY,{"derivedFrom":makeQuery(id+"F11.opPattern","COPY",BODY,{"derivedFrom":makeQuery(id+"F8.opPattern","COPY",BODY,{"derivedFrom":makeQuery(id+"F4.opPattern","COPY",BODY,{"derivedFrom":makeQuery(id+"F2.opPattern","COPY",BODY,{"derivedFrom":makeQuery(id+"F1.opRevolve","SWEPT_BODY",BODY,{"disambiguationData":[OSD([sQuery(id+"F0.wireOp",EDGE,"E1")])]}),"instanceName":"1"}),"instanceName":"1"}),"instanceName":"1"}),"instanceName":"1"}),"instanceName":"1"});
            var Q1204;
            Q1204=makeQuery(id+"F12.opPattern","COPY",BODY,{"derivedFrom":makeQuery(id+"F11.opPattern","COPY",BODY,{"derivedFrom":makeQuery(id+"F8.opPattern","COPY",BODY,{"derivedFrom":makeQuery(id+"F4.opPattern","COPY",BODY,{"derivedFrom":makeQuery(id+"F3.opPattern","COPY",BODY,{"derivedFrom":makeQuery(id+"F2.opPattern","COPY",BODY,{"derivedFrom":makeQuery(id+"F1.opRevolve","SWEPT_BODY",BODY,{"disambiguationData":[OSD([sQuery(id+"F0.wireOp",EDGE,"E1")])]}),"instanceName":"1"}),"instanceName":"1"}),"instanceName":"1"}),"instanceName":"1"}),"instanceName":"1"}),"instanceName":"1"});
            var Q1205;
            Q1205=makeQuery(id+"F12.opPattern","COPY",BODY,{"derivedFrom":makeQuery(id+"F11.opPattern","COPY",BODY,{"derivedFrom":makeQuery(id+"F8.opPattern","COPY",BODY,{"derivedFrom":makeQuery(id+"F5.opPattern","COPY",BODY,{"derivedFrom":makeQuery(id+"F1.opRevolve","SWEPT_BODY",BODY,{"disambiguationData":[OSD([sQuery(id+"F0.wireOp",EDGE,"E1")])]}),"instanceName":"1"}),"instanceName":"1"}),"instanceName":"1"}),"instanceName":"1"});
            var Q1206;
            Q1206=makeQuery(id+"F12.opPattern","COPY",BODY,{"derivedFrom":makeQuery(id+"F11.opPattern","COPY",BODY,{"derivedFrom":makeQuery(id+"F8.opPattern","COPY",BODY,{"derivedFrom":makeQuery(id+"F5.opPattern","COPY",BODY,{"derivedFrom":makeQuery(id+"F2.opPattern","COPY",BODY,{"derivedFrom":makeQuery(id+"F1.opRevolve","SWEPT_BODY",BODY,{"disambiguationData":[OSD([sQuery(id+"F0.wireOp",EDGE,"E1")])]}),"instanceName":"1"}),"instanceName":"1"}),"instanceName":"1"}),"instanceName":"1"}),"instanceName":"1"});
            var Q1207;
            Q1207=makeQuery(id+"F12.opPattern","COPY",BODY,{"derivedFrom":makeQuery(id+"F11.opPattern","COPY",BODY,{"derivedFrom":makeQuery(id+"F8.opPattern","COPY",BODY,{"derivedFrom":makeQuery(id+"F5.opPattern","COPY",BODY,{"derivedFrom":makeQuery(id+"F3.opPattern","COPY",BODY,{"derivedFrom":makeQuery(id+"F2.opPattern","COPY",BODY,{"derivedFrom":makeQuery(id+"F1.opRevolve","SWEPT_BODY",BODY,{"disambiguationData":[OSD([sQuery(id+"F0.wireOp",EDGE,"E1")])]}),"instanceName":"1"}),"instanceName":"1"}),"instanceName":"1"}),"instanceName":"1"}),"instanceName":"1"}),"instanceName":"1"});
            var Q1208;
            Q1208=makeQuery(id+"F12.opPattern","COPY",BODY,{"derivedFrom":makeQuery(id+"F11.opPattern","COPY",BODY,{"derivedFrom":makeQuery(id+"F8.opPattern","COPY",BODY,{"derivedFrom":makeQuery(id+"F5.opPattern","COPY",BODY,{"derivedFrom":makeQuery(id+"F4.opPattern","COPY",BODY,{"derivedFrom":makeQuery(id+"F1.opRevolve","SWEPT_BODY",BODY,{"disambiguationData":[OSD([sQuery(id+"F0.wireOp",EDGE,"E1")])]}),"instanceName":"1"}),"instanceName":"1"}),"instanceName":"1"}),"instanceName":"1"}),"instanceName":"1"});
            var Q1209;
            Q1209=makeQuery(id+"F12.opPattern","COPY",BODY,{"derivedFrom":makeQuery(id+"F11.opPattern","COPY",BODY,{"derivedFrom":makeQuery(id+"F8.opPattern","COPY",BODY,{"derivedFrom":makeQuery(id+"F5.opPattern","COPY",BODY,{"derivedFrom":makeQuery(id+"F4.opPattern","COPY",BODY,{"derivedFrom":makeQuery(id+"F2.opPattern","COPY",BODY,{"derivedFrom":makeQuery(id+"F1.opRevolve","SWEPT_BODY",BODY,{"disambiguationData":[OSD([sQuery(id+"F0.wireOp",EDGE,"E1")])]}),"instanceName":"1"}),"instanceName":"1"}),"instanceName":"1"}),"instanceName":"1"}),"instanceName":"1"}),"instanceName":"1"});
            var Q1210;
            Q1210=makeQuery(id+"F12.opPattern","COPY",BODY,{"derivedFrom":makeQuery(id+"F11.opPattern","COPY",BODY,{"derivedFrom":makeQuery(id+"F8.opPattern","COPY",BODY,{"derivedFrom":makeQuery(id+"F5.opPattern","COPY",BODY,{"derivedFrom":makeQuery(id+"F4.opPattern","COPY",BODY,{"derivedFrom":makeQuery(id+"F3.opPattern","COPY",BODY,{"derivedFrom":makeQuery(id+"F2.opPattern","COPY",BODY,{"derivedFrom":makeQuery(id+"F1.opRevolve","SWEPT_BODY",BODY,{"disambiguationData":[OSD([sQuery(id+"F0.wireOp",EDGE,"E1")])]}),"instanceName":"1"}),"instanceName":"1"}),"instanceName":"1"}),"instanceName":"1"}),"instanceName":"1"}),"instanceName":"1"}),"instanceName":"1"});
            var Q1211;
            Q1211=makeQuery(id+"F12.opPattern","COPY",BODY,{"derivedFrom":makeQuery(id+"F11.opPattern","COPY",BODY,{"derivedFrom":makeQuery(id+"F8.opPattern","COPY",BODY,{"derivedFrom":makeQuery(id+"F6.opPattern","COPY",BODY,{"derivedFrom":makeQuery(id+"F1.opRevolve","SWEPT_BODY",BODY,{"disambiguationData":[OSD([sQuery(id+"F0.wireOp",EDGE,"E1")])]}),"instanceName":"1"}),"instanceName":"1"}),"instanceName":"1"}),"instanceName":"1"});
            var Q1212;
            Q1212=makeQuery(id+"F12.opPattern","COPY",BODY,{"derivedFrom":makeQuery(id+"F11.opPattern","COPY",BODY,{"derivedFrom":makeQuery(id+"F8.opPattern","COPY",BODY,{"derivedFrom":makeQuery(id+"F6.opPattern","COPY",BODY,{"derivedFrom":makeQuery(id+"F2.opPattern","COPY",BODY,{"derivedFrom":makeQuery(id+"F1.opRevolve","SWEPT_BODY",BODY,{"disambiguationData":[OSD([sQuery(id+"F0.wireOp",EDGE,"E1")])]}),"instanceName":"1"}),"instanceName":"1"}),"instanceName":"1"}),"instanceName":"1"}),"instanceName":"1"});
            var Q1213;
            Q1213=makeQuery(id+"F12.opPattern","COPY",BODY,{"derivedFrom":makeQuery(id+"F11.opPattern","COPY",BODY,{"derivedFrom":makeQuery(id+"F8.opPattern","COPY",BODY,{"derivedFrom":makeQuery(id+"F6.opPattern","COPY",BODY,{"derivedFrom":makeQuery(id+"F3.opPattern","COPY",BODY,{"derivedFrom":makeQuery(id+"F2.opPattern","COPY",BODY,{"derivedFrom":makeQuery(id+"F1.opRevolve","SWEPT_BODY",BODY,{"disambiguationData":[OSD([sQuery(id+"F0.wireOp",EDGE,"E1")])]}),"instanceName":"1"}),"instanceName":"1"}),"instanceName":"1"}),"instanceName":"1"}),"instanceName":"1"}),"instanceName":"1"});
            var Q1214;
            Q1214=makeQuery(id+"F12.opPattern","COPY",BODY,{"derivedFrom":makeQuery(id+"F11.opPattern","COPY",BODY,{"derivedFrom":makeQuery(id+"F8.opPattern","COPY",BODY,{"derivedFrom":makeQuery(id+"F6.opPattern","COPY",BODY,{"derivedFrom":makeQuery(id+"F4.opPattern","COPY",BODY,{"derivedFrom":makeQuery(id+"F1.opRevolve","SWEPT_BODY",BODY,{"disambiguationData":[OSD([sQuery(id+"F0.wireOp",EDGE,"E1")])]}),"instanceName":"1"}),"instanceName":"1"}),"instanceName":"1"}),"instanceName":"1"}),"instanceName":"1"});
            var Q1215;
            Q1215=makeQuery(id+"F12.opPattern","COPY",BODY,{"derivedFrom":makeQuery(id+"F11.opPattern","COPY",BODY,{"derivedFrom":makeQuery(id+"F8.opPattern","COPY",BODY,{"derivedFrom":makeQuery(id+"F6.opPattern","COPY",BODY,{"derivedFrom":makeQuery(id+"F4.opPattern","COPY",BODY,{"derivedFrom":makeQuery(id+"F2.opPattern","COPY",BODY,{"derivedFrom":makeQuery(id+"F1.opRevolve","SWEPT_BODY",BODY,{"disambiguationData":[OSD([sQuery(id+"F0.wireOp",EDGE,"E1")])]}),"instanceName":"1"}),"instanceName":"1"}),"instanceName":"1"}),"instanceName":"1"}),"instanceName":"1"}),"instanceName":"1"});
            var Q1216;
            Q1216=makeQuery(id+"F12.opPattern","COPY",BODY,{"derivedFrom":makeQuery(id+"F11.opPattern","COPY",BODY,{"derivedFrom":makeQuery(id+"F8.opPattern","COPY",BODY,{"derivedFrom":makeQuery(id+"F6.opPattern","COPY",BODY,{"derivedFrom":makeQuery(id+"F4.opPattern","COPY",BODY,{"derivedFrom":makeQuery(id+"F3.opPattern","COPY",BODY,{"derivedFrom":makeQuery(id+"F2.opPattern","COPY",BODY,{"derivedFrom":makeQuery(id+"F1.opRevolve","SWEPT_BODY",BODY,{"disambiguationData":[OSD([sQuery(id+"F0.wireOp",EDGE,"E1")])]}),"instanceName":"1"}),"instanceName":"1"}),"instanceName":"1"}),"instanceName":"1"}),"instanceName":"1"}),"instanceName":"1"}),"instanceName":"1"});
            var Q1217;
            Q1217=makeQuery(id+"F12.opPattern","COPY",BODY,{"derivedFrom":makeQuery(id+"F11.opPattern","COPY",BODY,{"derivedFrom":makeQuery(id+"F8.opPattern","COPY",BODY,{"derivedFrom":makeQuery(id+"F6.opPattern","COPY",BODY,{"derivedFrom":makeQuery(id+"F5.opPattern","COPY",BODY,{"derivedFrom":makeQuery(id+"F1.opRevolve","SWEPT_BODY",BODY,{"disambiguationData":[OSD([sQuery(id+"F0.wireOp",EDGE,"E1")])]}),"instanceName":"1"}),"instanceName":"1"}),"instanceName":"1"}),"instanceName":"1"}),"instanceName":"1"});
            var Q1218;
            Q1218=makeQuery(id+"F12.opPattern","COPY",BODY,{"derivedFrom":makeQuery(id+"F11.opPattern","COPY",BODY,{"derivedFrom":makeQuery(id+"F8.opPattern","COPY",BODY,{"derivedFrom":makeQuery(id+"F6.opPattern","COPY",BODY,{"derivedFrom":makeQuery(id+"F5.opPattern","COPY",BODY,{"derivedFrom":makeQuery(id+"F2.opPattern","COPY",BODY,{"derivedFrom":makeQuery(id+"F1.opRevolve","SWEPT_BODY",BODY,{"disambiguationData":[OSD([sQuery(id+"F0.wireOp",EDGE,"E1")])]}),"instanceName":"1"}),"instanceName":"1"}),"instanceName":"1"}),"instanceName":"1"}),"instanceName":"1"}),"instanceName":"1"});
            var Q1219;
            Q1219=makeQuery(id+"F12.opPattern","COPY",BODY,{"derivedFrom":makeQuery(id+"F11.opPattern","COPY",BODY,{"derivedFrom":makeQuery(id+"F8.opPattern","COPY",BODY,{"derivedFrom":makeQuery(id+"F6.opPattern","COPY",BODY,{"derivedFrom":makeQuery(id+"F5.opPattern","COPY",BODY,{"derivedFrom":makeQuery(id+"F3.opPattern","COPY",BODY,{"derivedFrom":makeQuery(id+"F2.opPattern","COPY",BODY,{"derivedFrom":makeQuery(id+"F1.opRevolve","SWEPT_BODY",BODY,{"disambiguationData":[OSD([sQuery(id+"F0.wireOp",EDGE,"E1")])]}),"instanceName":"1"}),"instanceName":"1"}),"instanceName":"1"}),"instanceName":"1"}),"instanceName":"1"}),"instanceName":"1"}),"instanceName":"1"});
            var Q1220;
            Q1220=makeQuery(id+"F12.opPattern","COPY",BODY,{"derivedFrom":makeQuery(id+"F11.opPattern","COPY",BODY,{"derivedFrom":makeQuery(id+"F8.opPattern","COPY",BODY,{"derivedFrom":makeQuery(id+"F6.opPattern","COPY",BODY,{"derivedFrom":makeQuery(id+"F5.opPattern","COPY",BODY,{"derivedFrom":makeQuery(id+"F4.opPattern","COPY",BODY,{"derivedFrom":makeQuery(id+"F1.opRevolve","SWEPT_BODY",BODY,{"disambiguationData":[OSD([sQuery(id+"F0.wireOp",EDGE,"E1")])]}),"instanceName":"1"}),"instanceName":"1"}),"instanceName":"1"}),"instanceName":"1"}),"instanceName":"1"}),"instanceName":"1"});
            var Q1221;
            Q1221=makeQuery(id+"F12.opPattern","COPY",BODY,{"derivedFrom":makeQuery(id+"F11.opPattern","COPY",BODY,{"derivedFrom":makeQuery(id+"F8.opPattern","COPY",BODY,{"derivedFrom":makeQuery(id+"F6.opPattern","COPY",BODY,{"derivedFrom":makeQuery(id+"F5.opPattern","COPY",BODY,{"derivedFrom":makeQuery(id+"F4.opPattern","COPY",BODY,{"derivedFrom":makeQuery(id+"F2.opPattern","COPY",BODY,{"derivedFrom":makeQuery(id+"F1.opRevolve","SWEPT_BODY",BODY,{"disambiguationData":[OSD([sQuery(id+"F0.wireOp",EDGE,"E1")])]}),"instanceName":"1"}),"instanceName":"1"}),"instanceName":"1"}),"instanceName":"1"}),"instanceName":"1"}),"instanceName":"1"}),"instanceName":"1"});
            var Q1222;
            Q1222=makeQuery(id+"F12.opPattern","COPY",BODY,{"derivedFrom":makeQuery(id+"F11.opPattern","COPY",BODY,{"derivedFrom":makeQuery(id+"F8.opPattern","COPY",BODY,{"derivedFrom":makeQuery(id+"F6.opPattern","COPY",BODY,{"derivedFrom":makeQuery(id+"F5.opPattern","COPY",BODY,{"derivedFrom":makeQuery(id+"F4.opPattern","COPY",BODY,{"derivedFrom":makeQuery(id+"F3.opPattern","COPY",BODY,{"derivedFrom":makeQuery(id+"F2.opPattern","COPY",BODY,{"derivedFrom":makeQuery(id+"F1.opRevolve","SWEPT_BODY",BODY,{"disambiguationData":[OSD([sQuery(id+"F0.wireOp",EDGE,"E1")])]}),"instanceName":"1"}),"instanceName":"1"}),"instanceName":"1"}),"instanceName":"1"}),"instanceName":"1"}),"instanceName":"1"}),"instanceName":"1"}),"instanceName":"1"});
            var Q1223;
            Q1223=makeQuery(id+"F12.opPattern","COPY",BODY,{"derivedFrom":makeQuery(id+"F11.opPattern","COPY",BODY,{"derivedFrom":makeQuery(id+"F8.opPattern","COPY",BODY,{"derivedFrom":makeQuery(id+"F7.opPattern","COPY",BODY,{"derivedFrom":makeQuery(id+"F1.opRevolve","SWEPT_BODY",BODY,{"disambiguationData":[OSD([sQuery(id+"F0.wireOp",EDGE,"E1")])]}),"instanceName":"1"}),"instanceName":"1"}),"instanceName":"1"}),"instanceName":"1"});
            var Q1224;
            Q1224=makeQuery(id+"F12.opPattern","COPY",BODY,{"derivedFrom":makeQuery(id+"F11.opPattern","COPY",BODY,{"derivedFrom":makeQuery(id+"F8.opPattern","COPY",BODY,{"derivedFrom":makeQuery(id+"F7.opPattern","COPY",BODY,{"derivedFrom":makeQuery(id+"F2.opPattern","COPY",BODY,{"derivedFrom":makeQuery(id+"F1.opRevolve","SWEPT_BODY",BODY,{"disambiguationData":[OSD([sQuery(id+"F0.wireOp",EDGE,"E1")])]}),"instanceName":"1"}),"instanceName":"1"}),"instanceName":"1"}),"instanceName":"1"}),"instanceName":"1"});
            var Q1225;
            Q1225=makeQuery(id+"F12.opPattern","COPY",BODY,{"derivedFrom":makeQuery(id+"F11.opPattern","COPY",BODY,{"derivedFrom":makeQuery(id+"F8.opPattern","COPY",BODY,{"derivedFrom":makeQuery(id+"F7.opPattern","COPY",BODY,{"derivedFrom":makeQuery(id+"F3.opPattern","COPY",BODY,{"derivedFrom":makeQuery(id+"F2.opPattern","COPY",BODY,{"derivedFrom":makeQuery(id+"F1.opRevolve","SWEPT_BODY",BODY,{"disambiguationData":[OSD([sQuery(id+"F0.wireOp",EDGE,"E1")])]}),"instanceName":"1"}),"instanceName":"1"}),"instanceName":"1"}),"instanceName":"1"}),"instanceName":"1"}),"instanceName":"1"});
            var Q1226;
            Q1226=makeQuery(id+"F12.opPattern","COPY",BODY,{"derivedFrom":makeQuery(id+"F11.opPattern","COPY",BODY,{"derivedFrom":makeQuery(id+"F8.opPattern","COPY",BODY,{"derivedFrom":makeQuery(id+"F7.opPattern","COPY",BODY,{"derivedFrom":makeQuery(id+"F4.opPattern","COPY",BODY,{"derivedFrom":makeQuery(id+"F1.opRevolve","SWEPT_BODY",BODY,{"disambiguationData":[OSD([sQuery(id+"F0.wireOp",EDGE,"E1")])]}),"instanceName":"1"}),"instanceName":"1"}),"instanceName":"1"}),"instanceName":"1"}),"instanceName":"1"});
            var Q1227;
            Q1227=makeQuery(id+"F12.opPattern","COPY",BODY,{"derivedFrom":makeQuery(id+"F11.opPattern","COPY",BODY,{"derivedFrom":makeQuery(id+"F8.opPattern","COPY",BODY,{"derivedFrom":makeQuery(id+"F7.opPattern","COPY",BODY,{"derivedFrom":makeQuery(id+"F4.opPattern","COPY",BODY,{"derivedFrom":makeQuery(id+"F2.opPattern","COPY",BODY,{"derivedFrom":makeQuery(id+"F1.opRevolve","SWEPT_BODY",BODY,{"disambiguationData":[OSD([sQuery(id+"F0.wireOp",EDGE,"E1")])]}),"instanceName":"1"}),"instanceName":"1"}),"instanceName":"1"}),"instanceName":"1"}),"instanceName":"1"}),"instanceName":"1"});
            var Q1228;
            Q1228=makeQuery(id+"F12.opPattern","COPY",BODY,{"derivedFrom":makeQuery(id+"F11.opPattern","COPY",BODY,{"derivedFrom":makeQuery(id+"F8.opPattern","COPY",BODY,{"derivedFrom":makeQuery(id+"F7.opPattern","COPY",BODY,{"derivedFrom":makeQuery(id+"F4.opPattern","COPY",BODY,{"derivedFrom":makeQuery(id+"F3.opPattern","COPY",BODY,{"derivedFrom":makeQuery(id+"F2.opPattern","COPY",BODY,{"derivedFrom":makeQuery(id+"F1.opRevolve","SWEPT_BODY",BODY,{"disambiguationData":[OSD([sQuery(id+"F0.wireOp",EDGE,"E1")])]}),"instanceName":"1"}),"instanceName":"1"}),"instanceName":"1"}),"instanceName":"1"}),"instanceName":"1"}),"instanceName":"1"}),"instanceName":"1"});
            var Q1229;
            Q1229=makeQuery(id+"F12.opPattern","COPY",BODY,{"derivedFrom":makeQuery(id+"F11.opPattern","COPY",BODY,{"derivedFrom":makeQuery(id+"F8.opPattern","COPY",BODY,{"derivedFrom":makeQuery(id+"F7.opPattern","COPY",BODY,{"derivedFrom":makeQuery(id+"F5.opPattern","COPY",BODY,{"derivedFrom":makeQuery(id+"F1.opRevolve","SWEPT_BODY",BODY,{"disambiguationData":[OSD([sQuery(id+"F0.wireOp",EDGE,"E1")])]}),"instanceName":"1"}),"instanceName":"1"}),"instanceName":"1"}),"instanceName":"1"}),"instanceName":"1"});
            var Q1230;
            Q1230=makeQuery(id+"F12.opPattern","COPY",BODY,{"derivedFrom":makeQuery(id+"F11.opPattern","COPY",BODY,{"derivedFrom":makeQuery(id+"F8.opPattern","COPY",BODY,{"derivedFrom":makeQuery(id+"F7.opPattern","COPY",BODY,{"derivedFrom":makeQuery(id+"F5.opPattern","COPY",BODY,{"derivedFrom":makeQuery(id+"F2.opPattern","COPY",BODY,{"derivedFrom":makeQuery(id+"F1.opRevolve","SWEPT_BODY",BODY,{"disambiguationData":[OSD([sQuery(id+"F0.wireOp",EDGE,"E1")])]}),"instanceName":"1"}),"instanceName":"1"}),"instanceName":"1"}),"instanceName":"1"}),"instanceName":"1"}),"instanceName":"1"});
            var Q1231;
            Q1231=makeQuery(id+"F12.opPattern","COPY",BODY,{"derivedFrom":makeQuery(id+"F11.opPattern","COPY",BODY,{"derivedFrom":makeQuery(id+"F8.opPattern","COPY",BODY,{"derivedFrom":makeQuery(id+"F7.opPattern","COPY",BODY,{"derivedFrom":makeQuery(id+"F5.opPattern","COPY",BODY,{"derivedFrom":makeQuery(id+"F3.opPattern","COPY",BODY,{"derivedFrom":makeQuery(id+"F2.opPattern","COPY",BODY,{"derivedFrom":makeQuery(id+"F1.opRevolve","SWEPT_BODY",BODY,{"disambiguationData":[OSD([sQuery(id+"F0.wireOp",EDGE,"E1")])]}),"instanceName":"1"}),"instanceName":"1"}),"instanceName":"1"}),"instanceName":"1"}),"instanceName":"1"}),"instanceName":"1"}),"instanceName":"1"});
            var Q1232;
            Q1232=makeQuery(id+"F12.opPattern","COPY",BODY,{"derivedFrom":makeQuery(id+"F11.opPattern","COPY",BODY,{"derivedFrom":makeQuery(id+"F8.opPattern","COPY",BODY,{"derivedFrom":makeQuery(id+"F7.opPattern","COPY",BODY,{"derivedFrom":makeQuery(id+"F5.opPattern","COPY",BODY,{"derivedFrom":makeQuery(id+"F4.opPattern","COPY",BODY,{"derivedFrom":makeQuery(id+"F1.opRevolve","SWEPT_BODY",BODY,{"disambiguationData":[OSD([sQuery(id+"F0.wireOp",EDGE,"E1")])]}),"instanceName":"1"}),"instanceName":"1"}),"instanceName":"1"}),"instanceName":"1"}),"instanceName":"1"}),"instanceName":"1"});
            var Q1233;
            Q1233=makeQuery(id+"F12.opPattern","COPY",BODY,{"derivedFrom":makeQuery(id+"F11.opPattern","COPY",BODY,{"derivedFrom":makeQuery(id+"F8.opPattern","COPY",BODY,{"derivedFrom":makeQuery(id+"F7.opPattern","COPY",BODY,{"derivedFrom":makeQuery(id+"F5.opPattern","COPY",BODY,{"derivedFrom":makeQuery(id+"F4.opPattern","COPY",BODY,{"derivedFrom":makeQuery(id+"F2.opPattern","COPY",BODY,{"derivedFrom":makeQuery(id+"F1.opRevolve","SWEPT_BODY",BODY,{"disambiguationData":[OSD([sQuery(id+"F0.wireOp",EDGE,"E1")])]}),"instanceName":"1"}),"instanceName":"1"}),"instanceName":"1"}),"instanceName":"1"}),"instanceName":"1"}),"instanceName":"1"}),"instanceName":"1"});
            var Q1234;
            Q1234=makeQuery(id+"F12.opPattern","COPY",BODY,{"derivedFrom":makeQuery(id+"F11.opPattern","COPY",BODY,{"derivedFrom":makeQuery(id+"F8.opPattern","COPY",BODY,{"derivedFrom":makeQuery(id+"F7.opPattern","COPY",BODY,{"derivedFrom":makeQuery(id+"F5.opPattern","COPY",BODY,{"derivedFrom":makeQuery(id+"F4.opPattern","COPY",BODY,{"derivedFrom":makeQuery(id+"F3.opPattern","COPY",BODY,{"derivedFrom":makeQuery(id+"F2.opPattern","COPY",BODY,{"derivedFrom":makeQuery(id+"F1.opRevolve","SWEPT_BODY",BODY,{"disambiguationData":[OSD([sQuery(id+"F0.wireOp",EDGE,"E1")])]}),"instanceName":"1"}),"instanceName":"1"}),"instanceName":"1"}),"instanceName":"1"}),"instanceName":"1"}),"instanceName":"1"}),"instanceName":"1"}),"instanceName":"1"});
            var Q1235;
            Q1235=makeQuery(id+"F12.opPattern","COPY",BODY,{"derivedFrom":makeQuery(id+"F11.opPattern","COPY",BODY,{"derivedFrom":makeQuery(id+"F8.opPattern","COPY",BODY,{"derivedFrom":makeQuery(id+"F7.opPattern","COPY",BODY,{"derivedFrom":makeQuery(id+"F6.opPattern","COPY",BODY,{"derivedFrom":makeQuery(id+"F1.opRevolve","SWEPT_BODY",BODY,{"disambiguationData":[OSD([sQuery(id+"F0.wireOp",EDGE,"E1")])]}),"instanceName":"1"}),"instanceName":"1"}),"instanceName":"1"}),"instanceName":"1"}),"instanceName":"1"});
            var Q1236;
            Q1236=makeQuery(id+"F12.opPattern","COPY",BODY,{"derivedFrom":makeQuery(id+"F11.opPattern","COPY",BODY,{"derivedFrom":makeQuery(id+"F8.opPattern","COPY",BODY,{"derivedFrom":makeQuery(id+"F7.opPattern","COPY",BODY,{"derivedFrom":makeQuery(id+"F6.opPattern","COPY",BODY,{"derivedFrom":makeQuery(id+"F2.opPattern","COPY",BODY,{"derivedFrom":makeQuery(id+"F1.opRevolve","SWEPT_BODY",BODY,{"disambiguationData":[OSD([sQuery(id+"F0.wireOp",EDGE,"E1")])]}),"instanceName":"1"}),"instanceName":"1"}),"instanceName":"1"}),"instanceName":"1"}),"instanceName":"1"}),"instanceName":"1"});
            var Q1237;
            Q1237=makeQuery(id+"F12.opPattern","COPY",BODY,{"derivedFrom":makeQuery(id+"F11.opPattern","COPY",BODY,{"derivedFrom":makeQuery(id+"F8.opPattern","COPY",BODY,{"derivedFrom":makeQuery(id+"F7.opPattern","COPY",BODY,{"derivedFrom":makeQuery(id+"F6.opPattern","COPY",BODY,{"derivedFrom":makeQuery(id+"F3.opPattern","COPY",BODY,{"derivedFrom":makeQuery(id+"F2.opPattern","COPY",BODY,{"derivedFrom":makeQuery(id+"F1.opRevolve","SWEPT_BODY",BODY,{"disambiguationData":[OSD([sQuery(id+"F0.wireOp",EDGE,"E1")])]}),"instanceName":"1"}),"instanceName":"1"}),"instanceName":"1"}),"instanceName":"1"}),"instanceName":"1"}),"instanceName":"1"}),"instanceName":"1"});
            var Q1238;
            Q1238=makeQuery(id+"F12.opPattern","COPY",BODY,{"derivedFrom":makeQuery(id+"F11.opPattern","COPY",BODY,{"derivedFrom":makeQuery(id+"F8.opPattern","COPY",BODY,{"derivedFrom":makeQuery(id+"F7.opPattern","COPY",BODY,{"derivedFrom":makeQuery(id+"F6.opPattern","COPY",BODY,{"derivedFrom":makeQuery(id+"F4.opPattern","COPY",BODY,{"derivedFrom":makeQuery(id+"F1.opRevolve","SWEPT_BODY",BODY,{"disambiguationData":[OSD([sQuery(id+"F0.wireOp",EDGE,"E1")])]}),"instanceName":"1"}),"instanceName":"1"}),"instanceName":"1"}),"instanceName":"1"}),"instanceName":"1"}),"instanceName":"1"});
            var Q1239;
            Q1239=makeQuery(id+"F12.opPattern","COPY",BODY,{"derivedFrom":makeQuery(id+"F11.opPattern","COPY",BODY,{"derivedFrom":makeQuery(id+"F8.opPattern","COPY",BODY,{"derivedFrom":makeQuery(id+"F7.opPattern","COPY",BODY,{"derivedFrom":makeQuery(id+"F6.opPattern","COPY",BODY,{"derivedFrom":makeQuery(id+"F4.opPattern","COPY",BODY,{"derivedFrom":makeQuery(id+"F2.opPattern","COPY",BODY,{"derivedFrom":makeQuery(id+"F1.opRevolve","SWEPT_BODY",BODY,{"disambiguationData":[OSD([sQuery(id+"F0.wireOp",EDGE,"E1")])]}),"instanceName":"1"}),"instanceName":"1"}),"instanceName":"1"}),"instanceName":"1"}),"instanceName":"1"}),"instanceName":"1"}),"instanceName":"1"});
            var Q1240;
            Q1240=makeQuery(id+"F12.opPattern","COPY",BODY,{"derivedFrom":makeQuery(id+"F11.opPattern","COPY",BODY,{"derivedFrom":makeQuery(id+"F8.opPattern","COPY",BODY,{"derivedFrom":makeQuery(id+"F7.opPattern","COPY",BODY,{"derivedFrom":makeQuery(id+"F6.opPattern","COPY",BODY,{"derivedFrom":makeQuery(id+"F4.opPattern","COPY",BODY,{"derivedFrom":makeQuery(id+"F3.opPattern","COPY",BODY,{"derivedFrom":makeQuery(id+"F2.opPattern","COPY",BODY,{"derivedFrom":makeQuery(id+"F1.opRevolve","SWEPT_BODY",BODY,{"disambiguationData":[OSD([sQuery(id+"F0.wireOp",EDGE,"E1")])]}),"instanceName":"1"}),"instanceName":"1"}),"instanceName":"1"}),"instanceName":"1"}),"instanceName":"1"}),"instanceName":"1"}),"instanceName":"1"}),"instanceName":"1"});
            var Q1241;
            Q1241=makeQuery(id+"F12.opPattern","COPY",BODY,{"derivedFrom":makeQuery(id+"F11.opPattern","COPY",BODY,{"derivedFrom":makeQuery(id+"F8.opPattern","COPY",BODY,{"derivedFrom":makeQuery(id+"F7.opPattern","COPY",BODY,{"derivedFrom":makeQuery(id+"F6.opPattern","COPY",BODY,{"derivedFrom":makeQuery(id+"F5.opPattern","COPY",BODY,{"derivedFrom":makeQuery(id+"F1.opRevolve","SWEPT_BODY",BODY,{"disambiguationData":[OSD([sQuery(id+"F0.wireOp",EDGE,"E1")])]}),"instanceName":"1"}),"instanceName":"1"}),"instanceName":"1"}),"instanceName":"1"}),"instanceName":"1"}),"instanceName":"1"});
            var Q1242;
            Q1242=makeQuery(id+"F12.opPattern","COPY",BODY,{"derivedFrom":makeQuery(id+"F11.opPattern","COPY",BODY,{"derivedFrom":makeQuery(id+"F8.opPattern","COPY",BODY,{"derivedFrom":makeQuery(id+"F7.opPattern","COPY",BODY,{"derivedFrom":makeQuery(id+"F6.opPattern","COPY",BODY,{"derivedFrom":makeQuery(id+"F5.opPattern","COPY",BODY,{"derivedFrom":makeQuery(id+"F2.opPattern","COPY",BODY,{"derivedFrom":makeQuery(id+"F1.opRevolve","SWEPT_BODY",BODY,{"disambiguationData":[OSD([sQuery(id+"F0.wireOp",EDGE,"E1")])]}),"instanceName":"1"}),"instanceName":"1"}),"instanceName":"1"}),"instanceName":"1"}),"instanceName":"1"}),"instanceName":"1"}),"instanceName":"1"});
            var Q1243;
            Q1243=makeQuery(id+"F12.opPattern","COPY",BODY,{"derivedFrom":makeQuery(id+"F11.opPattern","COPY",BODY,{"derivedFrom":makeQuery(id+"F8.opPattern","COPY",BODY,{"derivedFrom":makeQuery(id+"F7.opPattern","COPY",BODY,{"derivedFrom":makeQuery(id+"F6.opPattern","COPY",BODY,{"derivedFrom":makeQuery(id+"F5.opPattern","COPY",BODY,{"derivedFrom":makeQuery(id+"F3.opPattern","COPY",BODY,{"derivedFrom":makeQuery(id+"F2.opPattern","COPY",BODY,{"derivedFrom":makeQuery(id+"F1.opRevolve","SWEPT_BODY",BODY,{"disambiguationData":[OSD([sQuery(id+"F0.wireOp",EDGE,"E1")])]}),"instanceName":"1"}),"instanceName":"1"}),"instanceName":"1"}),"instanceName":"1"}),"instanceName":"1"}),"instanceName":"1"}),"instanceName":"1"}),"instanceName":"1"});
            var Q1244;
            Q1244=makeQuery(id+"F12.opPattern","COPY",BODY,{"derivedFrom":makeQuery(id+"F11.opPattern","COPY",BODY,{"derivedFrom":makeQuery(id+"F8.opPattern","COPY",BODY,{"derivedFrom":makeQuery(id+"F7.opPattern","COPY",BODY,{"derivedFrom":makeQuery(id+"F6.opPattern","COPY",BODY,{"derivedFrom":makeQuery(id+"F5.opPattern","COPY",BODY,{"derivedFrom":makeQuery(id+"F4.opPattern","COPY",BODY,{"derivedFrom":makeQuery(id+"F1.opRevolve","SWEPT_BODY",BODY,{"disambiguationData":[OSD([sQuery(id+"F0.wireOp",EDGE,"E1")])]}),"instanceName":"1"}),"instanceName":"1"}),"instanceName":"1"}),"instanceName":"1"}),"instanceName":"1"}),"instanceName":"1"}),"instanceName":"1"});
            var Q1245;
            Q1245=makeQuery(id+"F12.opPattern","COPY",BODY,{"derivedFrom":makeQuery(id+"F11.opPattern","COPY",BODY,{"derivedFrom":makeQuery(id+"F8.opPattern","COPY",BODY,{"derivedFrom":makeQuery(id+"F7.opPattern","COPY",BODY,{"derivedFrom":makeQuery(id+"F6.opPattern","COPY",BODY,{"derivedFrom":makeQuery(id+"F5.opPattern","COPY",BODY,{"derivedFrom":makeQuery(id+"F4.opPattern","COPY",BODY,{"derivedFrom":makeQuery(id+"F2.opPattern","COPY",BODY,{"derivedFrom":makeQuery(id+"F1.opRevolve","SWEPT_BODY",BODY,{"disambiguationData":[OSD([sQuery(id+"F0.wireOp",EDGE,"E1")])]}),"instanceName":"1"}),"instanceName":"1"}),"instanceName":"1"}),"instanceName":"1"}),"instanceName":"1"}),"instanceName":"1"}),"instanceName":"1"}),"instanceName":"1"});
            var Q1246;
            Q1246=makeQuery(id+"F12.opPattern","COPY",BODY,{"derivedFrom":makeQuery(id+"F11.opPattern","COPY",BODY,{"derivedFrom":makeQuery(id+"F8.opPattern","COPY",BODY,{"derivedFrom":makeQuery(id+"F7.opPattern","COPY",BODY,{"derivedFrom":makeQuery(id+"F6.opPattern","COPY",BODY,{"derivedFrom":makeQuery(id+"F5.opPattern","COPY",BODY,{"derivedFrom":makeQuery(id+"F4.opPattern","COPY",BODY,{"derivedFrom":makeQuery(id+"F3.opPattern","COPY",BODY,{"derivedFrom":makeQuery(id+"F2.opPattern","COPY",BODY,{"derivedFrom":makeQuery(id+"F1.opRevolve","SWEPT_BODY",BODY,{"disambiguationData":[OSD([sQuery(id+"F0.wireOp",EDGE,"E1")])]}),"instanceName":"1"}),"instanceName":"1"}),"instanceName":"1"}),"instanceName":"1"}),"instanceName":"1"}),"instanceName":"1"}),"instanceName":"1"}),"instanceName":"1"}),"instanceName":"1"});
            var Q1247;
            Q1247=makeQuery(id+"F12.opPattern","COPY",BODY,{"derivedFrom":makeQuery(id+"F11.opPattern","COPY",BODY,{"derivedFrom":makeQuery(id+"F9.opPattern","COPY",BODY,{"derivedFrom":makeQuery(id+"F1.opRevolve","SWEPT_BODY",BODY,{"disambiguationData":[OSD([sQuery(id+"F0.wireOp",EDGE,"E1")])]}),"instanceName":"1"}),"instanceName":"1"}),"instanceName":"1"});
            var Q1248;
            Q1248=makeQuery(id+"F12.opPattern","COPY",BODY,{"derivedFrom":makeQuery(id+"F11.opPattern","COPY",BODY,{"derivedFrom":makeQuery(id+"F9.opPattern","COPY",BODY,{"derivedFrom":makeQuery(id+"F2.opPattern","COPY",BODY,{"derivedFrom":makeQuery(id+"F1.opRevolve","SWEPT_BODY",BODY,{"disambiguationData":[OSD([sQuery(id+"F0.wireOp",EDGE,"E1")])]}),"instanceName":"1"}),"instanceName":"1"}),"instanceName":"1"}),"instanceName":"1"});
            var Q1249;
            Q1249=makeQuery(id+"F12.opPattern","COPY",BODY,{"derivedFrom":makeQuery(id+"F11.opPattern","COPY",BODY,{"derivedFrom":makeQuery(id+"F9.opPattern","COPY",BODY,{"derivedFrom":makeQuery(id+"F3.opPattern","COPY",BODY,{"derivedFrom":makeQuery(id+"F2.opPattern","COPY",BODY,{"derivedFrom":makeQuery(id+"F1.opRevolve","SWEPT_BODY",BODY,{"disambiguationData":[OSD([sQuery(id+"F0.wireOp",EDGE,"E1")])]}),"instanceName":"1"}),"instanceName":"1"}),"instanceName":"1"}),"instanceName":"1"}),"instanceName":"1"});
            var Q1250;
            Q1250=makeQuery(id+"F12.opPattern","COPY",BODY,{"derivedFrom":makeQuery(id+"F11.opPattern","COPY",BODY,{"derivedFrom":makeQuery(id+"F9.opPattern","COPY",BODY,{"derivedFrom":makeQuery(id+"F4.opPattern","COPY",BODY,{"derivedFrom":makeQuery(id+"F1.opRevolve","SWEPT_BODY",BODY,{"disambiguationData":[OSD([sQuery(id+"F0.wireOp",EDGE,"E1")])]}),"instanceName":"1"}),"instanceName":"1"}),"instanceName":"1"}),"instanceName":"1"});
            var Q1251;
            Q1251=makeQuery(id+"F12.opPattern","COPY",BODY,{"derivedFrom":makeQuery(id+"F11.opPattern","COPY",BODY,{"derivedFrom":makeQuery(id+"F9.opPattern","COPY",BODY,{"derivedFrom":makeQuery(id+"F4.opPattern","COPY",BODY,{"derivedFrom":makeQuery(id+"F2.opPattern","COPY",BODY,{"derivedFrom":makeQuery(id+"F1.opRevolve","SWEPT_BODY",BODY,{"disambiguationData":[OSD([sQuery(id+"F0.wireOp",EDGE,"E1")])]}),"instanceName":"1"}),"instanceName":"1"}),"instanceName":"1"}),"instanceName":"1"}),"instanceName":"1"});
            var Q1252;
            Q1252=makeQuery(id+"F12.opPattern","COPY",BODY,{"derivedFrom":makeQuery(id+"F11.opPattern","COPY",BODY,{"derivedFrom":makeQuery(id+"F9.opPattern","COPY",BODY,{"derivedFrom":makeQuery(id+"F4.opPattern","COPY",BODY,{"derivedFrom":makeQuery(id+"F3.opPattern","COPY",BODY,{"derivedFrom":makeQuery(id+"F2.opPattern","COPY",BODY,{"derivedFrom":makeQuery(id+"F1.opRevolve","SWEPT_BODY",BODY,{"disambiguationData":[OSD([sQuery(id+"F0.wireOp",EDGE,"E1")])]}),"instanceName":"1"}),"instanceName":"1"}),"instanceName":"1"}),"instanceName":"1"}),"instanceName":"1"}),"instanceName":"1"});
            var Q1253;
            Q1253=makeQuery(id+"F12.opPattern","COPY",BODY,{"derivedFrom":makeQuery(id+"F11.opPattern","COPY",BODY,{"derivedFrom":makeQuery(id+"F9.opPattern","COPY",BODY,{"derivedFrom":makeQuery(id+"F5.opPattern","COPY",BODY,{"derivedFrom":makeQuery(id+"F1.opRevolve","SWEPT_BODY",BODY,{"disambiguationData":[OSD([sQuery(id+"F0.wireOp",EDGE,"E1")])]}),"instanceName":"1"}),"instanceName":"1"}),"instanceName":"1"}),"instanceName":"1"});
            var Q1254;
            Q1254=makeQuery(id+"F12.opPattern","COPY",BODY,{"derivedFrom":makeQuery(id+"F11.opPattern","COPY",BODY,{"derivedFrom":makeQuery(id+"F9.opPattern","COPY",BODY,{"derivedFrom":makeQuery(id+"F5.opPattern","COPY",BODY,{"derivedFrom":makeQuery(id+"F2.opPattern","COPY",BODY,{"derivedFrom":makeQuery(id+"F1.opRevolve","SWEPT_BODY",BODY,{"disambiguationData":[OSD([sQuery(id+"F0.wireOp",EDGE,"E1")])]}),"instanceName":"1"}),"instanceName":"1"}),"instanceName":"1"}),"instanceName":"1"}),"instanceName":"1"});
            var Q1255;
            Q1255=makeQuery(id+"F12.opPattern","COPY",BODY,{"derivedFrom":makeQuery(id+"F11.opPattern","COPY",BODY,{"derivedFrom":makeQuery(id+"F9.opPattern","COPY",BODY,{"derivedFrom":makeQuery(id+"F5.opPattern","COPY",BODY,{"derivedFrom":makeQuery(id+"F3.opPattern","COPY",BODY,{"derivedFrom":makeQuery(id+"F2.opPattern","COPY",BODY,{"derivedFrom":makeQuery(id+"F1.opRevolve","SWEPT_BODY",BODY,{"disambiguationData":[OSD([sQuery(id+"F0.wireOp",EDGE,"E1")])]}),"instanceName":"1"}),"instanceName":"1"}),"instanceName":"1"}),"instanceName":"1"}),"instanceName":"1"}),"instanceName":"1"});
            var Q1256;
            Q1256=makeQuery(id+"F12.opPattern","COPY",BODY,{"derivedFrom":makeQuery(id+"F11.opPattern","COPY",BODY,{"derivedFrom":makeQuery(id+"F9.opPattern","COPY",BODY,{"derivedFrom":makeQuery(id+"F5.opPattern","COPY",BODY,{"derivedFrom":makeQuery(id+"F4.opPattern","COPY",BODY,{"derivedFrom":makeQuery(id+"F1.opRevolve","SWEPT_BODY",BODY,{"disambiguationData":[OSD([sQuery(id+"F0.wireOp",EDGE,"E1")])]}),"instanceName":"1"}),"instanceName":"1"}),"instanceName":"1"}),"instanceName":"1"}),"instanceName":"1"});
            var Q1257;
            Q1257=makeQuery(id+"F12.opPattern","COPY",BODY,{"derivedFrom":makeQuery(id+"F11.opPattern","COPY",BODY,{"derivedFrom":makeQuery(id+"F9.opPattern","COPY",BODY,{"derivedFrom":makeQuery(id+"F5.opPattern","COPY",BODY,{"derivedFrom":makeQuery(id+"F4.opPattern","COPY",BODY,{"derivedFrom":makeQuery(id+"F2.opPattern","COPY",BODY,{"derivedFrom":makeQuery(id+"F1.opRevolve","SWEPT_BODY",BODY,{"disambiguationData":[OSD([sQuery(id+"F0.wireOp",EDGE,"E1")])]}),"instanceName":"1"}),"instanceName":"1"}),"instanceName":"1"}),"instanceName":"1"}),"instanceName":"1"}),"instanceName":"1"});
            var Q1258;
            Q1258=makeQuery(id+"F12.opPattern","COPY",BODY,{"derivedFrom":makeQuery(id+"F11.opPattern","COPY",BODY,{"derivedFrom":makeQuery(id+"F9.opPattern","COPY",BODY,{"derivedFrom":makeQuery(id+"F5.opPattern","COPY",BODY,{"derivedFrom":makeQuery(id+"F4.opPattern","COPY",BODY,{"derivedFrom":makeQuery(id+"F3.opPattern","COPY",BODY,{"derivedFrom":makeQuery(id+"F2.opPattern","COPY",BODY,{"derivedFrom":makeQuery(id+"F1.opRevolve","SWEPT_BODY",BODY,{"disambiguationData":[OSD([sQuery(id+"F0.wireOp",EDGE,"E1")])]}),"instanceName":"1"}),"instanceName":"1"}),"instanceName":"1"}),"instanceName":"1"}),"instanceName":"1"}),"instanceName":"1"}),"instanceName":"1"});
            var Q1259;
            Q1259=makeQuery(id+"F12.opPattern","COPY",BODY,{"derivedFrom":makeQuery(id+"F11.opPattern","COPY",BODY,{"derivedFrom":makeQuery(id+"F9.opPattern","COPY",BODY,{"derivedFrom":makeQuery(id+"F6.opPattern","COPY",BODY,{"derivedFrom":makeQuery(id+"F1.opRevolve","SWEPT_BODY",BODY,{"disambiguationData":[OSD([sQuery(id+"F0.wireOp",EDGE,"E1")])]}),"instanceName":"1"}),"instanceName":"1"}),"instanceName":"1"}),"instanceName":"1"});
            var Q1260;
            Q1260=makeQuery(id+"F12.opPattern","COPY",BODY,{"derivedFrom":makeQuery(id+"F11.opPattern","COPY",BODY,{"derivedFrom":makeQuery(id+"F9.opPattern","COPY",BODY,{"derivedFrom":makeQuery(id+"F6.opPattern","COPY",BODY,{"derivedFrom":makeQuery(id+"F2.opPattern","COPY",BODY,{"derivedFrom":makeQuery(id+"F1.opRevolve","SWEPT_BODY",BODY,{"disambiguationData":[OSD([sQuery(id+"F0.wireOp",EDGE,"E1")])]}),"instanceName":"1"}),"instanceName":"1"}),"instanceName":"1"}),"instanceName":"1"}),"instanceName":"1"});
            var Q1261;
            Q1261=makeQuery(id+"F12.opPattern","COPY",BODY,{"derivedFrom":makeQuery(id+"F11.opPattern","COPY",BODY,{"derivedFrom":makeQuery(id+"F9.opPattern","COPY",BODY,{"derivedFrom":makeQuery(id+"F6.opPattern","COPY",BODY,{"derivedFrom":makeQuery(id+"F3.opPattern","COPY",BODY,{"derivedFrom":makeQuery(id+"F2.opPattern","COPY",BODY,{"derivedFrom":makeQuery(id+"F1.opRevolve","SWEPT_BODY",BODY,{"disambiguationData":[OSD([sQuery(id+"F0.wireOp",EDGE,"E1")])]}),"instanceName":"1"}),"instanceName":"1"}),"instanceName":"1"}),"instanceName":"1"}),"instanceName":"1"}),"instanceName":"1"});
            var Q1262;
            Q1262=makeQuery(id+"F12.opPattern","COPY",BODY,{"derivedFrom":makeQuery(id+"F11.opPattern","COPY",BODY,{"derivedFrom":makeQuery(id+"F9.opPattern","COPY",BODY,{"derivedFrom":makeQuery(id+"F6.opPattern","COPY",BODY,{"derivedFrom":makeQuery(id+"F4.opPattern","COPY",BODY,{"derivedFrom":makeQuery(id+"F1.opRevolve","SWEPT_BODY",BODY,{"disambiguationData":[OSD([sQuery(id+"F0.wireOp",EDGE,"E1")])]}),"instanceName":"1"}),"instanceName":"1"}),"instanceName":"1"}),"instanceName":"1"}),"instanceName":"1"});
            var Q1263;
            Q1263=makeQuery(id+"F12.opPattern","COPY",BODY,{"derivedFrom":makeQuery(id+"F11.opPattern","COPY",BODY,{"derivedFrom":makeQuery(id+"F9.opPattern","COPY",BODY,{"derivedFrom":makeQuery(id+"F6.opPattern","COPY",BODY,{"derivedFrom":makeQuery(id+"F4.opPattern","COPY",BODY,{"derivedFrom":makeQuery(id+"F2.opPattern","COPY",BODY,{"derivedFrom":makeQuery(id+"F1.opRevolve","SWEPT_BODY",BODY,{"disambiguationData":[OSD([sQuery(id+"F0.wireOp",EDGE,"E1")])]}),"instanceName":"1"}),"instanceName":"1"}),"instanceName":"1"}),"instanceName":"1"}),"instanceName":"1"}),"instanceName":"1"});
            var Q1264;
            Q1264=makeQuery(id+"F12.opPattern","COPY",BODY,{"derivedFrom":makeQuery(id+"F11.opPattern","COPY",BODY,{"derivedFrom":makeQuery(id+"F9.opPattern","COPY",BODY,{"derivedFrom":makeQuery(id+"F6.opPattern","COPY",BODY,{"derivedFrom":makeQuery(id+"F4.opPattern","COPY",BODY,{"derivedFrom":makeQuery(id+"F3.opPattern","COPY",BODY,{"derivedFrom":makeQuery(id+"F2.opPattern","COPY",BODY,{"derivedFrom":makeQuery(id+"F1.opRevolve","SWEPT_BODY",BODY,{"disambiguationData":[OSD([sQuery(id+"F0.wireOp",EDGE,"E1")])]}),"instanceName":"1"}),"instanceName":"1"}),"instanceName":"1"}),"instanceName":"1"}),"instanceName":"1"}),"instanceName":"1"}),"instanceName":"1"});
            var Q1265;
            Q1265=makeQuery(id+"F12.opPattern","COPY",BODY,{"derivedFrom":makeQuery(id+"F11.opPattern","COPY",BODY,{"derivedFrom":makeQuery(id+"F9.opPattern","COPY",BODY,{"derivedFrom":makeQuery(id+"F6.opPattern","COPY",BODY,{"derivedFrom":makeQuery(id+"F5.opPattern","COPY",BODY,{"derivedFrom":makeQuery(id+"F1.opRevolve","SWEPT_BODY",BODY,{"disambiguationData":[OSD([sQuery(id+"F0.wireOp",EDGE,"E1")])]}),"instanceName":"1"}),"instanceName":"1"}),"instanceName":"1"}),"instanceName":"1"}),"instanceName":"1"});
            var Q1266;
            Q1266=makeQuery(id+"F12.opPattern","COPY",BODY,{"derivedFrom":makeQuery(id+"F11.opPattern","COPY",BODY,{"derivedFrom":makeQuery(id+"F9.opPattern","COPY",BODY,{"derivedFrom":makeQuery(id+"F6.opPattern","COPY",BODY,{"derivedFrom":makeQuery(id+"F5.opPattern","COPY",BODY,{"derivedFrom":makeQuery(id+"F2.opPattern","COPY",BODY,{"derivedFrom":makeQuery(id+"F1.opRevolve","SWEPT_BODY",BODY,{"disambiguationData":[OSD([sQuery(id+"F0.wireOp",EDGE,"E1")])]}),"instanceName":"1"}),"instanceName":"1"}),"instanceName":"1"}),"instanceName":"1"}),"instanceName":"1"}),"instanceName":"1"});
            var Q1267;
            Q1267=makeQuery(id+"F12.opPattern","COPY",BODY,{"derivedFrom":makeQuery(id+"F11.opPattern","COPY",BODY,{"derivedFrom":makeQuery(id+"F9.opPattern","COPY",BODY,{"derivedFrom":makeQuery(id+"F6.opPattern","COPY",BODY,{"derivedFrom":makeQuery(id+"F5.opPattern","COPY",BODY,{"derivedFrom":makeQuery(id+"F3.opPattern","COPY",BODY,{"derivedFrom":makeQuery(id+"F2.opPattern","COPY",BODY,{"derivedFrom":makeQuery(id+"F1.opRevolve","SWEPT_BODY",BODY,{"disambiguationData":[OSD([sQuery(id+"F0.wireOp",EDGE,"E1")])]}),"instanceName":"1"}),"instanceName":"1"}),"instanceName":"1"}),"instanceName":"1"}),"instanceName":"1"}),"instanceName":"1"}),"instanceName":"1"});
            var Q1268;
            Q1268=makeQuery(id+"F12.opPattern","COPY",BODY,{"derivedFrom":makeQuery(id+"F11.opPattern","COPY",BODY,{"derivedFrom":makeQuery(id+"F9.opPattern","COPY",BODY,{"derivedFrom":makeQuery(id+"F6.opPattern","COPY",BODY,{"derivedFrom":makeQuery(id+"F5.opPattern","COPY",BODY,{"derivedFrom":makeQuery(id+"F4.opPattern","COPY",BODY,{"derivedFrom":makeQuery(id+"F1.opRevolve","SWEPT_BODY",BODY,{"disambiguationData":[OSD([sQuery(id+"F0.wireOp",EDGE,"E1")])]}),"instanceName":"1"}),"instanceName":"1"}),"instanceName":"1"}),"instanceName":"1"}),"instanceName":"1"}),"instanceName":"1"});
            var Q1269;
            Q1269=makeQuery(id+"F12.opPattern","COPY",BODY,{"derivedFrom":makeQuery(id+"F11.opPattern","COPY",BODY,{"derivedFrom":makeQuery(id+"F9.opPattern","COPY",BODY,{"derivedFrom":makeQuery(id+"F6.opPattern","COPY",BODY,{"derivedFrom":makeQuery(id+"F5.opPattern","COPY",BODY,{"derivedFrom":makeQuery(id+"F4.opPattern","COPY",BODY,{"derivedFrom":makeQuery(id+"F2.opPattern","COPY",BODY,{"derivedFrom":makeQuery(id+"F1.opRevolve","SWEPT_BODY",BODY,{"disambiguationData":[OSD([sQuery(id+"F0.wireOp",EDGE,"E1")])]}),"instanceName":"1"}),"instanceName":"1"}),"instanceName":"1"}),"instanceName":"1"}),"instanceName":"1"}),"instanceName":"1"}),"instanceName":"1"});
            var Q1270;
            Q1270=makeQuery(id+"F12.opPattern","COPY",BODY,{"derivedFrom":makeQuery(id+"F11.opPattern","COPY",BODY,{"derivedFrom":makeQuery(id+"F9.opPattern","COPY",BODY,{"derivedFrom":makeQuery(id+"F6.opPattern","COPY",BODY,{"derivedFrom":makeQuery(id+"F5.opPattern","COPY",BODY,{"derivedFrom":makeQuery(id+"F4.opPattern","COPY",BODY,{"derivedFrom":makeQuery(id+"F3.opPattern","COPY",BODY,{"derivedFrom":makeQuery(id+"F2.opPattern","COPY",BODY,{"derivedFrom":makeQuery(id+"F1.opRevolve","SWEPT_BODY",BODY,{"disambiguationData":[OSD([sQuery(id+"F0.wireOp",EDGE,"E1")])]}),"instanceName":"1"}),"instanceName":"1"}),"instanceName":"1"}),"instanceName":"1"}),"instanceName":"1"}),"instanceName":"1"}),"instanceName":"1"}),"instanceName":"1"});
            var Q1271;
            Q1271=makeQuery(id+"F12.opPattern","COPY",BODY,{"derivedFrom":makeQuery(id+"F11.opPattern","COPY",BODY,{"derivedFrom":makeQuery(id+"F9.opPattern","COPY",BODY,{"derivedFrom":makeQuery(id+"F7.opPattern","COPY",BODY,{"derivedFrom":makeQuery(id+"F1.opRevolve","SWEPT_BODY",BODY,{"disambiguationData":[OSD([sQuery(id+"F0.wireOp",EDGE,"E1")])]}),"instanceName":"1"}),"instanceName":"1"}),"instanceName":"1"}),"instanceName":"1"});
            var Q1272;
            Q1272=makeQuery(id+"F12.opPattern","COPY",BODY,{"derivedFrom":makeQuery(id+"F11.opPattern","COPY",BODY,{"derivedFrom":makeQuery(id+"F9.opPattern","COPY",BODY,{"derivedFrom":makeQuery(id+"F7.opPattern","COPY",BODY,{"derivedFrom":makeQuery(id+"F2.opPattern","COPY",BODY,{"derivedFrom":makeQuery(id+"F1.opRevolve","SWEPT_BODY",BODY,{"disambiguationData":[OSD([sQuery(id+"F0.wireOp",EDGE,"E1")])]}),"instanceName":"1"}),"instanceName":"1"}),"instanceName":"1"}),"instanceName":"1"}),"instanceName":"1"});
            var Q1273;
            Q1273=makeQuery(id+"F12.opPattern","COPY",BODY,{"derivedFrom":makeQuery(id+"F11.opPattern","COPY",BODY,{"derivedFrom":makeQuery(id+"F9.opPattern","COPY",BODY,{"derivedFrom":makeQuery(id+"F7.opPattern","COPY",BODY,{"derivedFrom":makeQuery(id+"F3.opPattern","COPY",BODY,{"derivedFrom":makeQuery(id+"F2.opPattern","COPY",BODY,{"derivedFrom":makeQuery(id+"F1.opRevolve","SWEPT_BODY",BODY,{"disambiguationData":[OSD([sQuery(id+"F0.wireOp",EDGE,"E1")])]}),"instanceName":"1"}),"instanceName":"1"}),"instanceName":"1"}),"instanceName":"1"}),"instanceName":"1"}),"instanceName":"1"});
            var Q1274;
            Q1274=makeQuery(id+"F12.opPattern","COPY",BODY,{"derivedFrom":makeQuery(id+"F11.opPattern","COPY",BODY,{"derivedFrom":makeQuery(id+"F9.opPattern","COPY",BODY,{"derivedFrom":makeQuery(id+"F7.opPattern","COPY",BODY,{"derivedFrom":makeQuery(id+"F4.opPattern","COPY",BODY,{"derivedFrom":makeQuery(id+"F1.opRevolve","SWEPT_BODY",BODY,{"disambiguationData":[OSD([sQuery(id+"F0.wireOp",EDGE,"E1")])]}),"instanceName":"1"}),"instanceName":"1"}),"instanceName":"1"}),"instanceName":"1"}),"instanceName":"1"});
            var Q1275;
            Q1275=makeQuery(id+"F12.opPattern","COPY",BODY,{"derivedFrom":makeQuery(id+"F11.opPattern","COPY",BODY,{"derivedFrom":makeQuery(id+"F9.opPattern","COPY",BODY,{"derivedFrom":makeQuery(id+"F7.opPattern","COPY",BODY,{"derivedFrom":makeQuery(id+"F4.opPattern","COPY",BODY,{"derivedFrom":makeQuery(id+"F2.opPattern","COPY",BODY,{"derivedFrom":makeQuery(id+"F1.opRevolve","SWEPT_BODY",BODY,{"disambiguationData":[OSD([sQuery(id+"F0.wireOp",EDGE,"E1")])]}),"instanceName":"1"}),"instanceName":"1"}),"instanceName":"1"}),"instanceName":"1"}),"instanceName":"1"}),"instanceName":"1"});
            var Q1276;
            Q1276=makeQuery(id+"F12.opPattern","COPY",BODY,{"derivedFrom":makeQuery(id+"F11.opPattern","COPY",BODY,{"derivedFrom":makeQuery(id+"F9.opPattern","COPY",BODY,{"derivedFrom":makeQuery(id+"F7.opPattern","COPY",BODY,{"derivedFrom":makeQuery(id+"F4.opPattern","COPY",BODY,{"derivedFrom":makeQuery(id+"F3.opPattern","COPY",BODY,{"derivedFrom":makeQuery(id+"F2.opPattern","COPY",BODY,{"derivedFrom":makeQuery(id+"F1.opRevolve","SWEPT_BODY",BODY,{"disambiguationData":[OSD([sQuery(id+"F0.wireOp",EDGE,"E1")])]}),"instanceName":"1"}),"instanceName":"1"}),"instanceName":"1"}),"instanceName":"1"}),"instanceName":"1"}),"instanceName":"1"}),"instanceName":"1"});
            var Q1277;
            Q1277=makeQuery(id+"F12.opPattern","COPY",BODY,{"derivedFrom":makeQuery(id+"F11.opPattern","COPY",BODY,{"derivedFrom":makeQuery(id+"F9.opPattern","COPY",BODY,{"derivedFrom":makeQuery(id+"F7.opPattern","COPY",BODY,{"derivedFrom":makeQuery(id+"F5.opPattern","COPY",BODY,{"derivedFrom":makeQuery(id+"F1.opRevolve","SWEPT_BODY",BODY,{"disambiguationData":[OSD([sQuery(id+"F0.wireOp",EDGE,"E1")])]}),"instanceName":"1"}),"instanceName":"1"}),"instanceName":"1"}),"instanceName":"1"}),"instanceName":"1"});
            var Q1278;
            Q1278=makeQuery(id+"F12.opPattern","COPY",BODY,{"derivedFrom":makeQuery(id+"F11.opPattern","COPY",BODY,{"derivedFrom":makeQuery(id+"F9.opPattern","COPY",BODY,{"derivedFrom":makeQuery(id+"F7.opPattern","COPY",BODY,{"derivedFrom":makeQuery(id+"F5.opPattern","COPY",BODY,{"derivedFrom":makeQuery(id+"F2.opPattern","COPY",BODY,{"derivedFrom":makeQuery(id+"F1.opRevolve","SWEPT_BODY",BODY,{"disambiguationData":[OSD([sQuery(id+"F0.wireOp",EDGE,"E1")])]}),"instanceName":"1"}),"instanceName":"1"}),"instanceName":"1"}),"instanceName":"1"}),"instanceName":"1"}),"instanceName":"1"});
            var Q1279;
            Q1279=makeQuery(id+"F12.opPattern","COPY",BODY,{"derivedFrom":makeQuery(id+"F11.opPattern","COPY",BODY,{"derivedFrom":makeQuery(id+"F9.opPattern","COPY",BODY,{"derivedFrom":makeQuery(id+"F7.opPattern","COPY",BODY,{"derivedFrom":makeQuery(id+"F5.opPattern","COPY",BODY,{"derivedFrom":makeQuery(id+"F3.opPattern","COPY",BODY,{"derivedFrom":makeQuery(id+"F2.opPattern","COPY",BODY,{"derivedFrom":makeQuery(id+"F1.opRevolve","SWEPT_BODY",BODY,{"disambiguationData":[OSD([sQuery(id+"F0.wireOp",EDGE,"E1")])]}),"instanceName":"1"}),"instanceName":"1"}),"instanceName":"1"}),"instanceName":"1"}),"instanceName":"1"}),"instanceName":"1"}),"instanceName":"1"});
            var Q1280;
            Q1280=makeQuery(id+"F12.opPattern","COPY",BODY,{"derivedFrom":makeQuery(id+"F11.opPattern","COPY",BODY,{"derivedFrom":makeQuery(id+"F9.opPattern","COPY",BODY,{"derivedFrom":makeQuery(id+"F7.opPattern","COPY",BODY,{"derivedFrom":makeQuery(id+"F5.opPattern","COPY",BODY,{"derivedFrom":makeQuery(id+"F4.opPattern","COPY",BODY,{"derivedFrom":makeQuery(id+"F1.opRevolve","SWEPT_BODY",BODY,{"disambiguationData":[OSD([sQuery(id+"F0.wireOp",EDGE,"E1")])]}),"instanceName":"1"}),"instanceName":"1"}),"instanceName":"1"}),"instanceName":"1"}),"instanceName":"1"}),"instanceName":"1"});
            var Q1281;
            Q1281=makeQuery(id+"F12.opPattern","COPY",BODY,{"derivedFrom":makeQuery(id+"F11.opPattern","COPY",BODY,{"derivedFrom":makeQuery(id+"F9.opPattern","COPY",BODY,{"derivedFrom":makeQuery(id+"F7.opPattern","COPY",BODY,{"derivedFrom":makeQuery(id+"F5.opPattern","COPY",BODY,{"derivedFrom":makeQuery(id+"F4.opPattern","COPY",BODY,{"derivedFrom":makeQuery(id+"F2.opPattern","COPY",BODY,{"derivedFrom":makeQuery(id+"F1.opRevolve","SWEPT_BODY",BODY,{"disambiguationData":[OSD([sQuery(id+"F0.wireOp",EDGE,"E1")])]}),"instanceName":"1"}),"instanceName":"1"}),"instanceName":"1"}),"instanceName":"1"}),"instanceName":"1"}),"instanceName":"1"}),"instanceName":"1"});
            var Q1282;
            Q1282=makeQuery(id+"F12.opPattern","COPY",BODY,{"derivedFrom":makeQuery(id+"F11.opPattern","COPY",BODY,{"derivedFrom":makeQuery(id+"F9.opPattern","COPY",BODY,{"derivedFrom":makeQuery(id+"F7.opPattern","COPY",BODY,{"derivedFrom":makeQuery(id+"F5.opPattern","COPY",BODY,{"derivedFrom":makeQuery(id+"F4.opPattern","COPY",BODY,{"derivedFrom":makeQuery(id+"F3.opPattern","COPY",BODY,{"derivedFrom":makeQuery(id+"F2.opPattern","COPY",BODY,{"derivedFrom":makeQuery(id+"F1.opRevolve","SWEPT_BODY",BODY,{"disambiguationData":[OSD([sQuery(id+"F0.wireOp",EDGE,"E1")])]}),"instanceName":"1"}),"instanceName":"1"}),"instanceName":"1"}),"instanceName":"1"}),"instanceName":"1"}),"instanceName":"1"}),"instanceName":"1"}),"instanceName":"1"});
            var Q1283;
            Q1283=makeQuery(id+"F12.opPattern","COPY",BODY,{"derivedFrom":makeQuery(id+"F11.opPattern","COPY",BODY,{"derivedFrom":makeQuery(id+"F9.opPattern","COPY",BODY,{"derivedFrom":makeQuery(id+"F7.opPattern","COPY",BODY,{"derivedFrom":makeQuery(id+"F6.opPattern","COPY",BODY,{"derivedFrom":makeQuery(id+"F1.opRevolve","SWEPT_BODY",BODY,{"disambiguationData":[OSD([sQuery(id+"F0.wireOp",EDGE,"E1")])]}),"instanceName":"1"}),"instanceName":"1"}),"instanceName":"1"}),"instanceName":"1"}),"instanceName":"1"});
            var Q1284;
            Q1284=makeQuery(id+"F12.opPattern","COPY",BODY,{"derivedFrom":makeQuery(id+"F11.opPattern","COPY",BODY,{"derivedFrom":makeQuery(id+"F9.opPattern","COPY",BODY,{"derivedFrom":makeQuery(id+"F7.opPattern","COPY",BODY,{"derivedFrom":makeQuery(id+"F6.opPattern","COPY",BODY,{"derivedFrom":makeQuery(id+"F2.opPattern","COPY",BODY,{"derivedFrom":makeQuery(id+"F1.opRevolve","SWEPT_BODY",BODY,{"disambiguationData":[OSD([sQuery(id+"F0.wireOp",EDGE,"E1")])]}),"instanceName":"1"}),"instanceName":"1"}),"instanceName":"1"}),"instanceName":"1"}),"instanceName":"1"}),"instanceName":"1"});
            var Q1285;
            Q1285=makeQuery(id+"F12.opPattern","COPY",BODY,{"derivedFrom":makeQuery(id+"F11.opPattern","COPY",BODY,{"derivedFrom":makeQuery(id+"F9.opPattern","COPY",BODY,{"derivedFrom":makeQuery(id+"F7.opPattern","COPY",BODY,{"derivedFrom":makeQuery(id+"F6.opPattern","COPY",BODY,{"derivedFrom":makeQuery(id+"F3.opPattern","COPY",BODY,{"derivedFrom":makeQuery(id+"F2.opPattern","COPY",BODY,{"derivedFrom":makeQuery(id+"F1.opRevolve","SWEPT_BODY",BODY,{"disambiguationData":[OSD([sQuery(id+"F0.wireOp",EDGE,"E1")])]}),"instanceName":"1"}),"instanceName":"1"}),"instanceName":"1"}),"instanceName":"1"}),"instanceName":"1"}),"instanceName":"1"}),"instanceName":"1"});
            var Q1286;
            Q1286=makeQuery(id+"F12.opPattern","COPY",BODY,{"derivedFrom":makeQuery(id+"F11.opPattern","COPY",BODY,{"derivedFrom":makeQuery(id+"F9.opPattern","COPY",BODY,{"derivedFrom":makeQuery(id+"F7.opPattern","COPY",BODY,{"derivedFrom":makeQuery(id+"F6.opPattern","COPY",BODY,{"derivedFrom":makeQuery(id+"F4.opPattern","COPY",BODY,{"derivedFrom":makeQuery(id+"F1.opRevolve","SWEPT_BODY",BODY,{"disambiguationData":[OSD([sQuery(id+"F0.wireOp",EDGE,"E1")])]}),"instanceName":"1"}),"instanceName":"1"}),"instanceName":"1"}),"instanceName":"1"}),"instanceName":"1"}),"instanceName":"1"});
            var Q1287;
            Q1287=makeQuery(id+"F12.opPattern","COPY",BODY,{"derivedFrom":makeQuery(id+"F11.opPattern","COPY",BODY,{"derivedFrom":makeQuery(id+"F9.opPattern","COPY",BODY,{"derivedFrom":makeQuery(id+"F7.opPattern","COPY",BODY,{"derivedFrom":makeQuery(id+"F6.opPattern","COPY",BODY,{"derivedFrom":makeQuery(id+"F4.opPattern","COPY",BODY,{"derivedFrom":makeQuery(id+"F2.opPattern","COPY",BODY,{"derivedFrom":makeQuery(id+"F1.opRevolve","SWEPT_BODY",BODY,{"disambiguationData":[OSD([sQuery(id+"F0.wireOp",EDGE,"E1")])]}),"instanceName":"1"}),"instanceName":"1"}),"instanceName":"1"}),"instanceName":"1"}),"instanceName":"1"}),"instanceName":"1"}),"instanceName":"1"});
            var Q1288;
            Q1288=makeQuery(id+"F12.opPattern","COPY",BODY,{"derivedFrom":makeQuery(id+"F11.opPattern","COPY",BODY,{"derivedFrom":makeQuery(id+"F9.opPattern","COPY",BODY,{"derivedFrom":makeQuery(id+"F7.opPattern","COPY",BODY,{"derivedFrom":makeQuery(id+"F6.opPattern","COPY",BODY,{"derivedFrom":makeQuery(id+"F4.opPattern","COPY",BODY,{"derivedFrom":makeQuery(id+"F3.opPattern","COPY",BODY,{"derivedFrom":makeQuery(id+"F2.opPattern","COPY",BODY,{"derivedFrom":makeQuery(id+"F1.opRevolve","SWEPT_BODY",BODY,{"disambiguationData":[OSD([sQuery(id+"F0.wireOp",EDGE,"E1")])]}),"instanceName":"1"}),"instanceName":"1"}),"instanceName":"1"}),"instanceName":"1"}),"instanceName":"1"}),"instanceName":"1"}),"instanceName":"1"}),"instanceName":"1"});
            var Q1289;
            Q1289=makeQuery(id+"F12.opPattern","COPY",BODY,{"derivedFrom":makeQuery(id+"F11.opPattern","COPY",BODY,{"derivedFrom":makeQuery(id+"F9.opPattern","COPY",BODY,{"derivedFrom":makeQuery(id+"F7.opPattern","COPY",BODY,{"derivedFrom":makeQuery(id+"F6.opPattern","COPY",BODY,{"derivedFrom":makeQuery(id+"F5.opPattern","COPY",BODY,{"derivedFrom":makeQuery(id+"F1.opRevolve","SWEPT_BODY",BODY,{"disambiguationData":[OSD([sQuery(id+"F0.wireOp",EDGE,"E1")])]}),"instanceName":"1"}),"instanceName":"1"}),"instanceName":"1"}),"instanceName":"1"}),"instanceName":"1"}),"instanceName":"1"});
            var Q1290;
            Q1290=makeQuery(id+"F12.opPattern","COPY",BODY,{"derivedFrom":makeQuery(id+"F11.opPattern","COPY",BODY,{"derivedFrom":makeQuery(id+"F9.opPattern","COPY",BODY,{"derivedFrom":makeQuery(id+"F7.opPattern","COPY",BODY,{"derivedFrom":makeQuery(id+"F6.opPattern","COPY",BODY,{"derivedFrom":makeQuery(id+"F5.opPattern","COPY",BODY,{"derivedFrom":makeQuery(id+"F2.opPattern","COPY",BODY,{"derivedFrom":makeQuery(id+"F1.opRevolve","SWEPT_BODY",BODY,{"disambiguationData":[OSD([sQuery(id+"F0.wireOp",EDGE,"E1")])]}),"instanceName":"1"}),"instanceName":"1"}),"instanceName":"1"}),"instanceName":"1"}),"instanceName":"1"}),"instanceName":"1"}),"instanceName":"1"});
            var Q1291;
            Q1291=makeQuery(id+"F12.opPattern","COPY",BODY,{"derivedFrom":makeQuery(id+"F11.opPattern","COPY",BODY,{"derivedFrom":makeQuery(id+"F9.opPattern","COPY",BODY,{"derivedFrom":makeQuery(id+"F7.opPattern","COPY",BODY,{"derivedFrom":makeQuery(id+"F6.opPattern","COPY",BODY,{"derivedFrom":makeQuery(id+"F5.opPattern","COPY",BODY,{"derivedFrom":makeQuery(id+"F3.opPattern","COPY",BODY,{"derivedFrom":makeQuery(id+"F2.opPattern","COPY",BODY,{"derivedFrom":makeQuery(id+"F1.opRevolve","SWEPT_BODY",BODY,{"disambiguationData":[OSD([sQuery(id+"F0.wireOp",EDGE,"E1")])]}),"instanceName":"1"}),"instanceName":"1"}),"instanceName":"1"}),"instanceName":"1"}),"instanceName":"1"}),"instanceName":"1"}),"instanceName":"1"}),"instanceName":"1"});
            var Q1292;
            Q1292=makeQuery(id+"F12.opPattern","COPY",BODY,{"derivedFrom":makeQuery(id+"F11.opPattern","COPY",BODY,{"derivedFrom":makeQuery(id+"F9.opPattern","COPY",BODY,{"derivedFrom":makeQuery(id+"F7.opPattern","COPY",BODY,{"derivedFrom":makeQuery(id+"F6.opPattern","COPY",BODY,{"derivedFrom":makeQuery(id+"F5.opPattern","COPY",BODY,{"derivedFrom":makeQuery(id+"F4.opPattern","COPY",BODY,{"derivedFrom":makeQuery(id+"F1.opRevolve","SWEPT_BODY",BODY,{"disambiguationData":[OSD([sQuery(id+"F0.wireOp",EDGE,"E1")])]}),"instanceName":"1"}),"instanceName":"1"}),"instanceName":"1"}),"instanceName":"1"}),"instanceName":"1"}),"instanceName":"1"}),"instanceName":"1"});
            var Q1293;
            Q1293=makeQuery(id+"F12.opPattern","COPY",BODY,{"derivedFrom":makeQuery(id+"F11.opPattern","COPY",BODY,{"derivedFrom":makeQuery(id+"F9.opPattern","COPY",BODY,{"derivedFrom":makeQuery(id+"F7.opPattern","COPY",BODY,{"derivedFrom":makeQuery(id+"F6.opPattern","COPY",BODY,{"derivedFrom":makeQuery(id+"F5.opPattern","COPY",BODY,{"derivedFrom":makeQuery(id+"F4.opPattern","COPY",BODY,{"derivedFrom":makeQuery(id+"F2.opPattern","COPY",BODY,{"derivedFrom":makeQuery(id+"F1.opRevolve","SWEPT_BODY",BODY,{"disambiguationData":[OSD([sQuery(id+"F0.wireOp",EDGE,"E1")])]}),"instanceName":"1"}),"instanceName":"1"}),"instanceName":"1"}),"instanceName":"1"}),"instanceName":"1"}),"instanceName":"1"}),"instanceName":"1"}),"instanceName":"1"});
            var Q1294;
            Q1294=makeQuery(id+"F12.opPattern","COPY",BODY,{"derivedFrom":makeQuery(id+"F11.opPattern","COPY",BODY,{"derivedFrom":makeQuery(id+"F9.opPattern","COPY",BODY,{"derivedFrom":makeQuery(id+"F7.opPattern","COPY",BODY,{"derivedFrom":makeQuery(id+"F6.opPattern","COPY",BODY,{"derivedFrom":makeQuery(id+"F5.opPattern","COPY",BODY,{"derivedFrom":makeQuery(id+"F4.opPattern","COPY",BODY,{"derivedFrom":makeQuery(id+"F3.opPattern","COPY",BODY,{"derivedFrom":makeQuery(id+"F2.opPattern","COPY",BODY,{"derivedFrom":makeQuery(id+"F1.opRevolve","SWEPT_BODY",BODY,{"disambiguationData":[OSD([sQuery(id+"F0.wireOp",EDGE,"E1")])]}),"instanceName":"1"}),"instanceName":"1"}),"instanceName":"1"}),"instanceName":"1"}),"instanceName":"1"}),"instanceName":"1"}),"instanceName":"1"}),"instanceName":"1"}),"instanceName":"1"});
            var Q1295;
            Q1295=makeQuery(id+"F12.opPattern","COPY",BODY,{"derivedFrom":makeQuery(id+"F11.opPattern","COPY",BODY,{"derivedFrom":makeQuery(id+"F9.opPattern","COPY",BODY,{"derivedFrom":makeQuery(id+"F8.opPattern","COPY",BODY,{"derivedFrom":makeQuery(id+"F1.opRevolve","SWEPT_BODY",BODY,{"disambiguationData":[OSD([sQuery(id+"F0.wireOp",EDGE,"E1")])]}),"instanceName":"1"}),"instanceName":"1"}),"instanceName":"1"}),"instanceName":"1"});
            var Q1296;
            Q1296=makeQuery(id+"F12.opPattern","COPY",BODY,{"derivedFrom":makeQuery(id+"F11.opPattern","COPY",BODY,{"derivedFrom":makeQuery(id+"F9.opPattern","COPY",BODY,{"derivedFrom":makeQuery(id+"F8.opPattern","COPY",BODY,{"derivedFrom":makeQuery(id+"F2.opPattern","COPY",BODY,{"derivedFrom":makeQuery(id+"F1.opRevolve","SWEPT_BODY",BODY,{"disambiguationData":[OSD([sQuery(id+"F0.wireOp",EDGE,"E1")])]}),"instanceName":"1"}),"instanceName":"1"}),"instanceName":"1"}),"instanceName":"1"}),"instanceName":"1"});
            var Q1297;
            Q1297=makeQuery(id+"F12.opPattern","COPY",BODY,{"derivedFrom":makeQuery(id+"F11.opPattern","COPY",BODY,{"derivedFrom":makeQuery(id+"F9.opPattern","COPY",BODY,{"derivedFrom":makeQuery(id+"F8.opPattern","COPY",BODY,{"derivedFrom":makeQuery(id+"F3.opPattern","COPY",BODY,{"derivedFrom":makeQuery(id+"F2.opPattern","COPY",BODY,{"derivedFrom":makeQuery(id+"F1.opRevolve","SWEPT_BODY",BODY,{"disambiguationData":[OSD([sQuery(id+"F0.wireOp",EDGE,"E1")])]}),"instanceName":"1"}),"instanceName":"1"}),"instanceName":"1"}),"instanceName":"1"}),"instanceName":"1"}),"instanceName":"1"});
            var Q1298;
            Q1298=makeQuery(id+"F12.opPattern","COPY",BODY,{"derivedFrom":makeQuery(id+"F11.opPattern","COPY",BODY,{"derivedFrom":makeQuery(id+"F9.opPattern","COPY",BODY,{"derivedFrom":makeQuery(id+"F8.opPattern","COPY",BODY,{"derivedFrom":makeQuery(id+"F4.opPattern","COPY",BODY,{"derivedFrom":makeQuery(id+"F1.opRevolve","SWEPT_BODY",BODY,{"disambiguationData":[OSD([sQuery(id+"F0.wireOp",EDGE,"E1")])]}),"instanceName":"1"}),"instanceName":"1"}),"instanceName":"1"}),"instanceName":"1"}),"instanceName":"1"});
            var Q1299;
            Q1299=makeQuery(id+"F12.opPattern","COPY",BODY,{"derivedFrom":makeQuery(id+"F11.opPattern","COPY",BODY,{"derivedFrom":makeQuery(id+"F9.opPattern","COPY",BODY,{"derivedFrom":makeQuery(id+"F8.opPattern","COPY",BODY,{"derivedFrom":makeQuery(id+"F4.opPattern","COPY",BODY,{"derivedFrom":makeQuery(id+"F2.opPattern","COPY",BODY,{"derivedFrom":makeQuery(id+"F1.opRevolve","SWEPT_BODY",BODY,{"disambiguationData":[OSD([sQuery(id+"F0.wireOp",EDGE,"E1")])]}),"instanceName":"1"}),"instanceName":"1"}),"instanceName":"1"}),"instanceName":"1"}),"instanceName":"1"}),"instanceName":"1"});
            var Q1300;
            Q1300=makeQuery(id+"F12.opPattern","COPY",BODY,{"derivedFrom":makeQuery(id+"F11.opPattern","COPY",BODY,{"derivedFrom":makeQuery(id+"F9.opPattern","COPY",BODY,{"derivedFrom":makeQuery(id+"F8.opPattern","COPY",BODY,{"derivedFrom":makeQuery(id+"F4.opPattern","COPY",BODY,{"derivedFrom":makeQuery(id+"F3.opPattern","COPY",BODY,{"derivedFrom":makeQuery(id+"F2.opPattern","COPY",BODY,{"derivedFrom":makeQuery(id+"F1.opRevolve","SWEPT_BODY",BODY,{"disambiguationData":[OSD([sQuery(id+"F0.wireOp",EDGE,"E1")])]}),"instanceName":"1"}),"instanceName":"1"}),"instanceName":"1"}),"instanceName":"1"}),"instanceName":"1"}),"instanceName":"1"}),"instanceName":"1"});
            var Q1301;
            Q1301=makeQuery(id+"F12.opPattern","COPY",BODY,{"derivedFrom":makeQuery(id+"F11.opPattern","COPY",BODY,{"derivedFrom":makeQuery(id+"F9.opPattern","COPY",BODY,{"derivedFrom":makeQuery(id+"F8.opPattern","COPY",BODY,{"derivedFrom":makeQuery(id+"F5.opPattern","COPY",BODY,{"derivedFrom":makeQuery(id+"F1.opRevolve","SWEPT_BODY",BODY,{"disambiguationData":[OSD([sQuery(id+"F0.wireOp",EDGE,"E1")])]}),"instanceName":"1"}),"instanceName":"1"}),"instanceName":"1"}),"instanceName":"1"}),"instanceName":"1"});
            var Q1302;
            Q1302=makeQuery(id+"F12.opPattern","COPY",BODY,{"derivedFrom":makeQuery(id+"F11.opPattern","COPY",BODY,{"derivedFrom":makeQuery(id+"F9.opPattern","COPY",BODY,{"derivedFrom":makeQuery(id+"F8.opPattern","COPY",BODY,{"derivedFrom":makeQuery(id+"F5.opPattern","COPY",BODY,{"derivedFrom":makeQuery(id+"F2.opPattern","COPY",BODY,{"derivedFrom":makeQuery(id+"F1.opRevolve","SWEPT_BODY",BODY,{"disambiguationData":[OSD([sQuery(id+"F0.wireOp",EDGE,"E1")])]}),"instanceName":"1"}),"instanceName":"1"}),"instanceName":"1"}),"instanceName":"1"}),"instanceName":"1"}),"instanceName":"1"});
            var Q1303;
            Q1303=makeQuery(id+"F12.opPattern","COPY",BODY,{"derivedFrom":makeQuery(id+"F11.opPattern","COPY",BODY,{"derivedFrom":makeQuery(id+"F9.opPattern","COPY",BODY,{"derivedFrom":makeQuery(id+"F8.opPattern","COPY",BODY,{"derivedFrom":makeQuery(id+"F5.opPattern","COPY",BODY,{"derivedFrom":makeQuery(id+"F3.opPattern","COPY",BODY,{"derivedFrom":makeQuery(id+"F2.opPattern","COPY",BODY,{"derivedFrom":makeQuery(id+"F1.opRevolve","SWEPT_BODY",BODY,{"disambiguationData":[OSD([sQuery(id+"F0.wireOp",EDGE,"E1")])]}),"instanceName":"1"}),"instanceName":"1"}),"instanceName":"1"}),"instanceName":"1"}),"instanceName":"1"}),"instanceName":"1"}),"instanceName":"1"});
            var Q1304;
            Q1304=makeQuery(id+"F12.opPattern","COPY",BODY,{"derivedFrom":makeQuery(id+"F11.opPattern","COPY",BODY,{"derivedFrom":makeQuery(id+"F9.opPattern","COPY",BODY,{"derivedFrom":makeQuery(id+"F8.opPattern","COPY",BODY,{"derivedFrom":makeQuery(id+"F5.opPattern","COPY",BODY,{"derivedFrom":makeQuery(id+"F4.opPattern","COPY",BODY,{"derivedFrom":makeQuery(id+"F1.opRevolve","SWEPT_BODY",BODY,{"disambiguationData":[OSD([sQuery(id+"F0.wireOp",EDGE,"E1")])]}),"instanceName":"1"}),"instanceName":"1"}),"instanceName":"1"}),"instanceName":"1"}),"instanceName":"1"}),"instanceName":"1"});
            var Q1305;
            Q1305=makeQuery(id+"F12.opPattern","COPY",BODY,{"derivedFrom":makeQuery(id+"F11.opPattern","COPY",BODY,{"derivedFrom":makeQuery(id+"F9.opPattern","COPY",BODY,{"derivedFrom":makeQuery(id+"F8.opPattern","COPY",BODY,{"derivedFrom":makeQuery(id+"F5.opPattern","COPY",BODY,{"derivedFrom":makeQuery(id+"F4.opPattern","COPY",BODY,{"derivedFrom":makeQuery(id+"F2.opPattern","COPY",BODY,{"derivedFrom":makeQuery(id+"F1.opRevolve","SWEPT_BODY",BODY,{"disambiguationData":[OSD([sQuery(id+"F0.wireOp",EDGE,"E1")])]}),"instanceName":"1"}),"instanceName":"1"}),"instanceName":"1"}),"instanceName":"1"}),"instanceName":"1"}),"instanceName":"1"}),"instanceName":"1"});
            var Q1306;
            Q1306=makeQuery(id+"F12.opPattern","COPY",BODY,{"derivedFrom":makeQuery(id+"F11.opPattern","COPY",BODY,{"derivedFrom":makeQuery(id+"F9.opPattern","COPY",BODY,{"derivedFrom":makeQuery(id+"F8.opPattern","COPY",BODY,{"derivedFrom":makeQuery(id+"F5.opPattern","COPY",BODY,{"derivedFrom":makeQuery(id+"F4.opPattern","COPY",BODY,{"derivedFrom":makeQuery(id+"F3.opPattern","COPY",BODY,{"derivedFrom":makeQuery(id+"F2.opPattern","COPY",BODY,{"derivedFrom":makeQuery(id+"F1.opRevolve","SWEPT_BODY",BODY,{"disambiguationData":[OSD([sQuery(id+"F0.wireOp",EDGE,"E1")])]}),"instanceName":"1"}),"instanceName":"1"}),"instanceName":"1"}),"instanceName":"1"}),"instanceName":"1"}),"instanceName":"1"}),"instanceName":"1"}),"instanceName":"1"});
            var Q1307;
            Q1307=makeQuery(id+"F12.opPattern","COPY",BODY,{"derivedFrom":makeQuery(id+"F11.opPattern","COPY",BODY,{"derivedFrom":makeQuery(id+"F9.opPattern","COPY",BODY,{"derivedFrom":makeQuery(id+"F8.opPattern","COPY",BODY,{"derivedFrom":makeQuery(id+"F6.opPattern","COPY",BODY,{"derivedFrom":makeQuery(id+"F1.opRevolve","SWEPT_BODY",BODY,{"disambiguationData":[OSD([sQuery(id+"F0.wireOp",EDGE,"E1")])]}),"instanceName":"1"}),"instanceName":"1"}),"instanceName":"1"}),"instanceName":"1"}),"instanceName":"1"});
            var Q1308;
            Q1308=makeQuery(id+"F12.opPattern","COPY",BODY,{"derivedFrom":makeQuery(id+"F11.opPattern","COPY",BODY,{"derivedFrom":makeQuery(id+"F9.opPattern","COPY",BODY,{"derivedFrom":makeQuery(id+"F8.opPattern","COPY",BODY,{"derivedFrom":makeQuery(id+"F6.opPattern","COPY",BODY,{"derivedFrom":makeQuery(id+"F2.opPattern","COPY",BODY,{"derivedFrom":makeQuery(id+"F1.opRevolve","SWEPT_BODY",BODY,{"disambiguationData":[OSD([sQuery(id+"F0.wireOp",EDGE,"E1")])]}),"instanceName":"1"}),"instanceName":"1"}),"instanceName":"1"}),"instanceName":"1"}),"instanceName":"1"}),"instanceName":"1"});
            var Q1309;
            Q1309=makeQuery(id+"F12.opPattern","COPY",BODY,{"derivedFrom":makeQuery(id+"F11.opPattern","COPY",BODY,{"derivedFrom":makeQuery(id+"F9.opPattern","COPY",BODY,{"derivedFrom":makeQuery(id+"F8.opPattern","COPY",BODY,{"derivedFrom":makeQuery(id+"F6.opPattern","COPY",BODY,{"derivedFrom":makeQuery(id+"F3.opPattern","COPY",BODY,{"derivedFrom":makeQuery(id+"F2.opPattern","COPY",BODY,{"derivedFrom":makeQuery(id+"F1.opRevolve","SWEPT_BODY",BODY,{"disambiguationData":[OSD([sQuery(id+"F0.wireOp",EDGE,"E1")])]}),"instanceName":"1"}),"instanceName":"1"}),"instanceName":"1"}),"instanceName":"1"}),"instanceName":"1"}),"instanceName":"1"}),"instanceName":"1"});
            var Q1310;
            Q1310=makeQuery(id+"F12.opPattern","COPY",BODY,{"derivedFrom":makeQuery(id+"F11.opPattern","COPY",BODY,{"derivedFrom":makeQuery(id+"F9.opPattern","COPY",BODY,{"derivedFrom":makeQuery(id+"F8.opPattern","COPY",BODY,{"derivedFrom":makeQuery(id+"F6.opPattern","COPY",BODY,{"derivedFrom":makeQuery(id+"F4.opPattern","COPY",BODY,{"derivedFrom":makeQuery(id+"F1.opRevolve","SWEPT_BODY",BODY,{"disambiguationData":[OSD([sQuery(id+"F0.wireOp",EDGE,"E1")])]}),"instanceName":"1"}),"instanceName":"1"}),"instanceName":"1"}),"instanceName":"1"}),"instanceName":"1"}),"instanceName":"1"});
            var Q1311;
            Q1311=makeQuery(id+"F12.opPattern","COPY",BODY,{"derivedFrom":makeQuery(id+"F11.opPattern","COPY",BODY,{"derivedFrom":makeQuery(id+"F9.opPattern","COPY",BODY,{"derivedFrom":makeQuery(id+"F8.opPattern","COPY",BODY,{"derivedFrom":makeQuery(id+"F6.opPattern","COPY",BODY,{"derivedFrom":makeQuery(id+"F4.opPattern","COPY",BODY,{"derivedFrom":makeQuery(id+"F2.opPattern","COPY",BODY,{"derivedFrom":makeQuery(id+"F1.opRevolve","SWEPT_BODY",BODY,{"disambiguationData":[OSD([sQuery(id+"F0.wireOp",EDGE,"E1")])]}),"instanceName":"1"}),"instanceName":"1"}),"instanceName":"1"}),"instanceName":"1"}),"instanceName":"1"}),"instanceName":"1"}),"instanceName":"1"});
            var Q1312;
            Q1312=makeQuery(id+"F12.opPattern","COPY",BODY,{"derivedFrom":makeQuery(id+"F11.opPattern","COPY",BODY,{"derivedFrom":makeQuery(id+"F9.opPattern","COPY",BODY,{"derivedFrom":makeQuery(id+"F8.opPattern","COPY",BODY,{"derivedFrom":makeQuery(id+"F6.opPattern","COPY",BODY,{"derivedFrom":makeQuery(id+"F4.opPattern","COPY",BODY,{"derivedFrom":makeQuery(id+"F3.opPattern","COPY",BODY,{"derivedFrom":makeQuery(id+"F2.opPattern","COPY",BODY,{"derivedFrom":makeQuery(id+"F1.opRevolve","SWEPT_BODY",BODY,{"disambiguationData":[OSD([sQuery(id+"F0.wireOp",EDGE,"E1")])]}),"instanceName":"1"}),"instanceName":"1"}),"instanceName":"1"}),"instanceName":"1"}),"instanceName":"1"}),"instanceName":"1"}),"instanceName":"1"}),"instanceName":"1"});
            var Q1313;
            Q1313=makeQuery(id+"F12.opPattern","COPY",BODY,{"derivedFrom":makeQuery(id+"F11.opPattern","COPY",BODY,{"derivedFrom":makeQuery(id+"F9.opPattern","COPY",BODY,{"derivedFrom":makeQuery(id+"F8.opPattern","COPY",BODY,{"derivedFrom":makeQuery(id+"F6.opPattern","COPY",BODY,{"derivedFrom":makeQuery(id+"F5.opPattern","COPY",BODY,{"derivedFrom":makeQuery(id+"F1.opRevolve","SWEPT_BODY",BODY,{"disambiguationData":[OSD([sQuery(id+"F0.wireOp",EDGE,"E1")])]}),"instanceName":"1"}),"instanceName":"1"}),"instanceName":"1"}),"instanceName":"1"}),"instanceName":"1"}),"instanceName":"1"});
            var Q1314;
            Q1314=makeQuery(id+"F12.opPattern","COPY",BODY,{"derivedFrom":makeQuery(id+"F11.opPattern","COPY",BODY,{"derivedFrom":makeQuery(id+"F9.opPattern","COPY",BODY,{"derivedFrom":makeQuery(id+"F8.opPattern","COPY",BODY,{"derivedFrom":makeQuery(id+"F6.opPattern","COPY",BODY,{"derivedFrom":makeQuery(id+"F5.opPattern","COPY",BODY,{"derivedFrom":makeQuery(id+"F2.opPattern","COPY",BODY,{"derivedFrom":makeQuery(id+"F1.opRevolve","SWEPT_BODY",BODY,{"disambiguationData":[OSD([sQuery(id+"F0.wireOp",EDGE,"E1")])]}),"instanceName":"1"}),"instanceName":"1"}),"instanceName":"1"}),"instanceName":"1"}),"instanceName":"1"}),"instanceName":"1"}),"instanceName":"1"});
            var Q1315;
            Q1315=makeQuery(id+"F12.opPattern","COPY",BODY,{"derivedFrom":makeQuery(id+"F11.opPattern","COPY",BODY,{"derivedFrom":makeQuery(id+"F9.opPattern","COPY",BODY,{"derivedFrom":makeQuery(id+"F8.opPattern","COPY",BODY,{"derivedFrom":makeQuery(id+"F6.opPattern","COPY",BODY,{"derivedFrom":makeQuery(id+"F5.opPattern","COPY",BODY,{"derivedFrom":makeQuery(id+"F3.opPattern","COPY",BODY,{"derivedFrom":makeQuery(id+"F2.opPattern","COPY",BODY,{"derivedFrom":makeQuery(id+"F1.opRevolve","SWEPT_BODY",BODY,{"disambiguationData":[OSD([sQuery(id+"F0.wireOp",EDGE,"E1")])]}),"instanceName":"1"}),"instanceName":"1"}),"instanceName":"1"}),"instanceName":"1"}),"instanceName":"1"}),"instanceName":"1"}),"instanceName":"1"}),"instanceName":"1"});
            var Q1316;
            Q1316=makeQuery(id+"F12.opPattern","COPY",BODY,{"derivedFrom":makeQuery(id+"F11.opPattern","COPY",BODY,{"derivedFrom":makeQuery(id+"F9.opPattern","COPY",BODY,{"derivedFrom":makeQuery(id+"F8.opPattern","COPY",BODY,{"derivedFrom":makeQuery(id+"F6.opPattern","COPY",BODY,{"derivedFrom":makeQuery(id+"F5.opPattern","COPY",BODY,{"derivedFrom":makeQuery(id+"F4.opPattern","COPY",BODY,{"derivedFrom":makeQuery(id+"F1.opRevolve","SWEPT_BODY",BODY,{"disambiguationData":[OSD([sQuery(id+"F0.wireOp",EDGE,"E1")])]}),"instanceName":"1"}),"instanceName":"1"}),"instanceName":"1"}),"instanceName":"1"}),"instanceName":"1"}),"instanceName":"1"}),"instanceName":"1"});
            var Q1317;
            Q1317=makeQuery(id+"F12.opPattern","COPY",BODY,{"derivedFrom":makeQuery(id+"F11.opPattern","COPY",BODY,{"derivedFrom":makeQuery(id+"F9.opPattern","COPY",BODY,{"derivedFrom":makeQuery(id+"F8.opPattern","COPY",BODY,{"derivedFrom":makeQuery(id+"F6.opPattern","COPY",BODY,{"derivedFrom":makeQuery(id+"F5.opPattern","COPY",BODY,{"derivedFrom":makeQuery(id+"F4.opPattern","COPY",BODY,{"derivedFrom":makeQuery(id+"F2.opPattern","COPY",BODY,{"derivedFrom":makeQuery(id+"F1.opRevolve","SWEPT_BODY",BODY,{"disambiguationData":[OSD([sQuery(id+"F0.wireOp",EDGE,"E1")])]}),"instanceName":"1"}),"instanceName":"1"}),"instanceName":"1"}),"instanceName":"1"}),"instanceName":"1"}),"instanceName":"1"}),"instanceName":"1"}),"instanceName":"1"});
            var Q1318;
            Q1318=makeQuery(id+"F12.opPattern","COPY",BODY,{"derivedFrom":makeQuery(id+"F11.opPattern","COPY",BODY,{"derivedFrom":makeQuery(id+"F9.opPattern","COPY",BODY,{"derivedFrom":makeQuery(id+"F8.opPattern","COPY",BODY,{"derivedFrom":makeQuery(id+"F6.opPattern","COPY",BODY,{"derivedFrom":makeQuery(id+"F5.opPattern","COPY",BODY,{"derivedFrom":makeQuery(id+"F4.opPattern","COPY",BODY,{"derivedFrom":makeQuery(id+"F3.opPattern","COPY",BODY,{"derivedFrom":makeQuery(id+"F2.opPattern","COPY",BODY,{"derivedFrom":makeQuery(id+"F1.opRevolve","SWEPT_BODY",BODY,{"disambiguationData":[OSD([sQuery(id+"F0.wireOp",EDGE,"E1")])]}),"instanceName":"1"}),"instanceName":"1"}),"instanceName":"1"}),"instanceName":"1"}),"instanceName":"1"}),"instanceName":"1"}),"instanceName":"1"}),"instanceName":"1"}),"instanceName":"1"});
            var Q1319;
            Q1319=makeQuery(id+"F12.opPattern","COPY",BODY,{"derivedFrom":makeQuery(id+"F11.opPattern","COPY",BODY,{"derivedFrom":makeQuery(id+"F9.opPattern","COPY",BODY,{"derivedFrom":makeQuery(id+"F8.opPattern","COPY",BODY,{"derivedFrom":makeQuery(id+"F7.opPattern","COPY",BODY,{"derivedFrom":makeQuery(id+"F1.opRevolve","SWEPT_BODY",BODY,{"disambiguationData":[OSD([sQuery(id+"F0.wireOp",EDGE,"E1")])]}),"instanceName":"1"}),"instanceName":"1"}),"instanceName":"1"}),"instanceName":"1"}),"instanceName":"1"});
            var Q1320;
            Q1320=makeQuery(id+"F12.opPattern","COPY",BODY,{"derivedFrom":makeQuery(id+"F11.opPattern","COPY",BODY,{"derivedFrom":makeQuery(id+"F9.opPattern","COPY",BODY,{"derivedFrom":makeQuery(id+"F8.opPattern","COPY",BODY,{"derivedFrom":makeQuery(id+"F7.opPattern","COPY",BODY,{"derivedFrom":makeQuery(id+"F2.opPattern","COPY",BODY,{"derivedFrom":makeQuery(id+"F1.opRevolve","SWEPT_BODY",BODY,{"disambiguationData":[OSD([sQuery(id+"F0.wireOp",EDGE,"E1")])]}),"instanceName":"1"}),"instanceName":"1"}),"instanceName":"1"}),"instanceName":"1"}),"instanceName":"1"}),"instanceName":"1"});
            var Q1321;
            Q1321=makeQuery(id+"F12.opPattern","COPY",BODY,{"derivedFrom":makeQuery(id+"F11.opPattern","COPY",BODY,{"derivedFrom":makeQuery(id+"F9.opPattern","COPY",BODY,{"derivedFrom":makeQuery(id+"F8.opPattern","COPY",BODY,{"derivedFrom":makeQuery(id+"F7.opPattern","COPY",BODY,{"derivedFrom":makeQuery(id+"F3.opPattern","COPY",BODY,{"derivedFrom":makeQuery(id+"F2.opPattern","COPY",BODY,{"derivedFrom":makeQuery(id+"F1.opRevolve","SWEPT_BODY",BODY,{"disambiguationData":[OSD([sQuery(id+"F0.wireOp",EDGE,"E1")])]}),"instanceName":"1"}),"instanceName":"1"}),"instanceName":"1"}),"instanceName":"1"}),"instanceName":"1"}),"instanceName":"1"}),"instanceName":"1"});
            var Q1322;
            Q1322=makeQuery(id+"F12.opPattern","COPY",BODY,{"derivedFrom":makeQuery(id+"F11.opPattern","COPY",BODY,{"derivedFrom":makeQuery(id+"F9.opPattern","COPY",BODY,{"derivedFrom":makeQuery(id+"F8.opPattern","COPY",BODY,{"derivedFrom":makeQuery(id+"F7.opPattern","COPY",BODY,{"derivedFrom":makeQuery(id+"F4.opPattern","COPY",BODY,{"derivedFrom":makeQuery(id+"F1.opRevolve","SWEPT_BODY",BODY,{"disambiguationData":[OSD([sQuery(id+"F0.wireOp",EDGE,"E1")])]}),"instanceName":"1"}),"instanceName":"1"}),"instanceName":"1"}),"instanceName":"1"}),"instanceName":"1"}),"instanceName":"1"});
            var Q1323;
            Q1323=makeQuery(id+"F12.opPattern","COPY",BODY,{"derivedFrom":makeQuery(id+"F11.opPattern","COPY",BODY,{"derivedFrom":makeQuery(id+"F9.opPattern","COPY",BODY,{"derivedFrom":makeQuery(id+"F8.opPattern","COPY",BODY,{"derivedFrom":makeQuery(id+"F7.opPattern","COPY",BODY,{"derivedFrom":makeQuery(id+"F4.opPattern","COPY",BODY,{"derivedFrom":makeQuery(id+"F2.opPattern","COPY",BODY,{"derivedFrom":makeQuery(id+"F1.opRevolve","SWEPT_BODY",BODY,{"disambiguationData":[OSD([sQuery(id+"F0.wireOp",EDGE,"E1")])]}),"instanceName":"1"}),"instanceName":"1"}),"instanceName":"1"}),"instanceName":"1"}),"instanceName":"1"}),"instanceName":"1"}),"instanceName":"1"});
            var Q1324;
            Q1324=makeQuery(id+"F12.opPattern","COPY",BODY,{"derivedFrom":makeQuery(id+"F11.opPattern","COPY",BODY,{"derivedFrom":makeQuery(id+"F9.opPattern","COPY",BODY,{"derivedFrom":makeQuery(id+"F8.opPattern","COPY",BODY,{"derivedFrom":makeQuery(id+"F7.opPattern","COPY",BODY,{"derivedFrom":makeQuery(id+"F4.opPattern","COPY",BODY,{"derivedFrom":makeQuery(id+"F3.opPattern","COPY",BODY,{"derivedFrom":makeQuery(id+"F2.opPattern","COPY",BODY,{"derivedFrom":makeQuery(id+"F1.opRevolve","SWEPT_BODY",BODY,{"disambiguationData":[OSD([sQuery(id+"F0.wireOp",EDGE,"E1")])]}),"instanceName":"1"}),"instanceName":"1"}),"instanceName":"1"}),"instanceName":"1"}),"instanceName":"1"}),"instanceName":"1"}),"instanceName":"1"}),"instanceName":"1"});
            var Q1325;
            Q1325=makeQuery(id+"F12.opPattern","COPY",BODY,{"derivedFrom":makeQuery(id+"F11.opPattern","COPY",BODY,{"derivedFrom":makeQuery(id+"F9.opPattern","COPY",BODY,{"derivedFrom":makeQuery(id+"F8.opPattern","COPY",BODY,{"derivedFrom":makeQuery(id+"F7.opPattern","COPY",BODY,{"derivedFrom":makeQuery(id+"F5.opPattern","COPY",BODY,{"derivedFrom":makeQuery(id+"F1.opRevolve","SWEPT_BODY",BODY,{"disambiguationData":[OSD([sQuery(id+"F0.wireOp",EDGE,"E1")])]}),"instanceName":"1"}),"instanceName":"1"}),"instanceName":"1"}),"instanceName":"1"}),"instanceName":"1"}),"instanceName":"1"});
            var Q1326;
            Q1326=makeQuery(id+"F12.opPattern","COPY",BODY,{"derivedFrom":makeQuery(id+"F11.opPattern","COPY",BODY,{"derivedFrom":makeQuery(id+"F9.opPattern","COPY",BODY,{"derivedFrom":makeQuery(id+"F8.opPattern","COPY",BODY,{"derivedFrom":makeQuery(id+"F7.opPattern","COPY",BODY,{"derivedFrom":makeQuery(id+"F5.opPattern","COPY",BODY,{"derivedFrom":makeQuery(id+"F2.opPattern","COPY",BODY,{"derivedFrom":makeQuery(id+"F1.opRevolve","SWEPT_BODY",BODY,{"disambiguationData":[OSD([sQuery(id+"F0.wireOp",EDGE,"E1")])]}),"instanceName":"1"}),"instanceName":"1"}),"instanceName":"1"}),"instanceName":"1"}),"instanceName":"1"}),"instanceName":"1"}),"instanceName":"1"});
            var Q1327;
            Q1327=makeQuery(id+"F12.opPattern","COPY",BODY,{"derivedFrom":makeQuery(id+"F11.opPattern","COPY",BODY,{"derivedFrom":makeQuery(id+"F9.opPattern","COPY",BODY,{"derivedFrom":makeQuery(id+"F8.opPattern","COPY",BODY,{"derivedFrom":makeQuery(id+"F7.opPattern","COPY",BODY,{"derivedFrom":makeQuery(id+"F5.opPattern","COPY",BODY,{"derivedFrom":makeQuery(id+"F3.opPattern","COPY",BODY,{"derivedFrom":makeQuery(id+"F2.opPattern","COPY",BODY,{"derivedFrom":makeQuery(id+"F1.opRevolve","SWEPT_BODY",BODY,{"disambiguationData":[OSD([sQuery(id+"F0.wireOp",EDGE,"E1")])]}),"instanceName":"1"}),"instanceName":"1"}),"instanceName":"1"}),"instanceName":"1"}),"instanceName":"1"}),"instanceName":"1"}),"instanceName":"1"}),"instanceName":"1"});
            var Q1328;
            Q1328=makeQuery(id+"F12.opPattern","COPY",BODY,{"derivedFrom":makeQuery(id+"F11.opPattern","COPY",BODY,{"derivedFrom":makeQuery(id+"F9.opPattern","COPY",BODY,{"derivedFrom":makeQuery(id+"F8.opPattern","COPY",BODY,{"derivedFrom":makeQuery(id+"F7.opPattern","COPY",BODY,{"derivedFrom":makeQuery(id+"F5.opPattern","COPY",BODY,{"derivedFrom":makeQuery(id+"F4.opPattern","COPY",BODY,{"derivedFrom":makeQuery(id+"F1.opRevolve","SWEPT_BODY",BODY,{"disambiguationData":[OSD([sQuery(id+"F0.wireOp",EDGE,"E1")])]}),"instanceName":"1"}),"instanceName":"1"}),"instanceName":"1"}),"instanceName":"1"}),"instanceName":"1"}),"instanceName":"1"}),"instanceName":"1"});
            var Q1329;
            Q1329=makeQuery(id+"F12.opPattern","COPY",BODY,{"derivedFrom":makeQuery(id+"F11.opPattern","COPY",BODY,{"derivedFrom":makeQuery(id+"F9.opPattern","COPY",BODY,{"derivedFrom":makeQuery(id+"F8.opPattern","COPY",BODY,{"derivedFrom":makeQuery(id+"F7.opPattern","COPY",BODY,{"derivedFrom":makeQuery(id+"F5.opPattern","COPY",BODY,{"derivedFrom":makeQuery(id+"F4.opPattern","COPY",BODY,{"derivedFrom":makeQuery(id+"F2.opPattern","COPY",BODY,{"derivedFrom":makeQuery(id+"F1.opRevolve","SWEPT_BODY",BODY,{"disambiguationData":[OSD([sQuery(id+"F0.wireOp",EDGE,"E1")])]}),"instanceName":"1"}),"instanceName":"1"}),"instanceName":"1"}),"instanceName":"1"}),"instanceName":"1"}),"instanceName":"1"}),"instanceName":"1"}),"instanceName":"1"});
            var Q1330;
            Q1330=makeQuery(id+"F12.opPattern","COPY",BODY,{"derivedFrom":makeQuery(id+"F11.opPattern","COPY",BODY,{"derivedFrom":makeQuery(id+"F9.opPattern","COPY",BODY,{"derivedFrom":makeQuery(id+"F8.opPattern","COPY",BODY,{"derivedFrom":makeQuery(id+"F7.opPattern","COPY",BODY,{"derivedFrom":makeQuery(id+"F5.opPattern","COPY",BODY,{"derivedFrom":makeQuery(id+"F4.opPattern","COPY",BODY,{"derivedFrom":makeQuery(id+"F3.opPattern","COPY",BODY,{"derivedFrom":makeQuery(id+"F2.opPattern","COPY",BODY,{"derivedFrom":makeQuery(id+"F1.opRevolve","SWEPT_BODY",BODY,{"disambiguationData":[OSD([sQuery(id+"F0.wireOp",EDGE,"E1")])]}),"instanceName":"1"}),"instanceName":"1"}),"instanceName":"1"}),"instanceName":"1"}),"instanceName":"1"}),"instanceName":"1"}),"instanceName":"1"}),"instanceName":"1"}),"instanceName":"1"});
            var Q1331;
            Q1331=makeQuery(id+"F12.opPattern","COPY",BODY,{"derivedFrom":makeQuery(id+"F11.opPattern","COPY",BODY,{"derivedFrom":makeQuery(id+"F9.opPattern","COPY",BODY,{"derivedFrom":makeQuery(id+"F8.opPattern","COPY",BODY,{"derivedFrom":makeQuery(id+"F7.opPattern","COPY",BODY,{"derivedFrom":makeQuery(id+"F6.opPattern","COPY",BODY,{"derivedFrom":makeQuery(id+"F1.opRevolve","SWEPT_BODY",BODY,{"disambiguationData":[OSD([sQuery(id+"F0.wireOp",EDGE,"E1")])]}),"instanceName":"1"}),"instanceName":"1"}),"instanceName":"1"}),"instanceName":"1"}),"instanceName":"1"}),"instanceName":"1"});
            var Q1332;
            Q1332=makeQuery(id+"F12.opPattern","COPY",BODY,{"derivedFrom":makeQuery(id+"F11.opPattern","COPY",BODY,{"derivedFrom":makeQuery(id+"F9.opPattern","COPY",BODY,{"derivedFrom":makeQuery(id+"F8.opPattern","COPY",BODY,{"derivedFrom":makeQuery(id+"F7.opPattern","COPY",BODY,{"derivedFrom":makeQuery(id+"F6.opPattern","COPY",BODY,{"derivedFrom":makeQuery(id+"F2.opPattern","COPY",BODY,{"derivedFrom":makeQuery(id+"F1.opRevolve","SWEPT_BODY",BODY,{"disambiguationData":[OSD([sQuery(id+"F0.wireOp",EDGE,"E1")])]}),"instanceName":"1"}),"instanceName":"1"}),"instanceName":"1"}),"instanceName":"1"}),"instanceName":"1"}),"instanceName":"1"}),"instanceName":"1"});
            var Q1333;
            Q1333=makeQuery(id+"F12.opPattern","COPY",BODY,{"derivedFrom":makeQuery(id+"F11.opPattern","COPY",BODY,{"derivedFrom":makeQuery(id+"F9.opPattern","COPY",BODY,{"derivedFrom":makeQuery(id+"F8.opPattern","COPY",BODY,{"derivedFrom":makeQuery(id+"F7.opPattern","COPY",BODY,{"derivedFrom":makeQuery(id+"F6.opPattern","COPY",BODY,{"derivedFrom":makeQuery(id+"F3.opPattern","COPY",BODY,{"derivedFrom":makeQuery(id+"F2.opPattern","COPY",BODY,{"derivedFrom":makeQuery(id+"F1.opRevolve","SWEPT_BODY",BODY,{"disambiguationData":[OSD([sQuery(id+"F0.wireOp",EDGE,"E1")])]}),"instanceName":"1"}),"instanceName":"1"}),"instanceName":"1"}),"instanceName":"1"}),"instanceName":"1"}),"instanceName":"1"}),"instanceName":"1"}),"instanceName":"1"});
            var Q1334;
            Q1334=makeQuery(id+"F12.opPattern","COPY",BODY,{"derivedFrom":makeQuery(id+"F11.opPattern","COPY",BODY,{"derivedFrom":makeQuery(id+"F9.opPattern","COPY",BODY,{"derivedFrom":makeQuery(id+"F8.opPattern","COPY",BODY,{"derivedFrom":makeQuery(id+"F7.opPattern","COPY",BODY,{"derivedFrom":makeQuery(id+"F6.opPattern","COPY",BODY,{"derivedFrom":makeQuery(id+"F4.opPattern","COPY",BODY,{"derivedFrom":makeQuery(id+"F1.opRevolve","SWEPT_BODY",BODY,{"disambiguationData":[OSD([sQuery(id+"F0.wireOp",EDGE,"E1")])]}),"instanceName":"1"}),"instanceName":"1"}),"instanceName":"1"}),"instanceName":"1"}),"instanceName":"1"}),"instanceName":"1"}),"instanceName":"1"});
            var Q1335;
            Q1335=makeQuery(id+"F12.opPattern","COPY",BODY,{"derivedFrom":makeQuery(id+"F11.opPattern","COPY",BODY,{"derivedFrom":makeQuery(id+"F9.opPattern","COPY",BODY,{"derivedFrom":makeQuery(id+"F8.opPattern","COPY",BODY,{"derivedFrom":makeQuery(id+"F7.opPattern","COPY",BODY,{"derivedFrom":makeQuery(id+"F6.opPattern","COPY",BODY,{"derivedFrom":makeQuery(id+"F4.opPattern","COPY",BODY,{"derivedFrom":makeQuery(id+"F2.opPattern","COPY",BODY,{"derivedFrom":makeQuery(id+"F1.opRevolve","SWEPT_BODY",BODY,{"disambiguationData":[OSD([sQuery(id+"F0.wireOp",EDGE,"E1")])]}),"instanceName":"1"}),"instanceName":"1"}),"instanceName":"1"}),"instanceName":"1"}),"instanceName":"1"}),"instanceName":"1"}),"instanceName":"1"}),"instanceName":"1"});
            var Q1336;
            Q1336=makeQuery(id+"F12.opPattern","COPY",BODY,{"derivedFrom":makeQuery(id+"F11.opPattern","COPY",BODY,{"derivedFrom":makeQuery(id+"F9.opPattern","COPY",BODY,{"derivedFrom":makeQuery(id+"F8.opPattern","COPY",BODY,{"derivedFrom":makeQuery(id+"F7.opPattern","COPY",BODY,{"derivedFrom":makeQuery(id+"F6.opPattern","COPY",BODY,{"derivedFrom":makeQuery(id+"F4.opPattern","COPY",BODY,{"derivedFrom":makeQuery(id+"F3.opPattern","COPY",BODY,{"derivedFrom":makeQuery(id+"F2.opPattern","COPY",BODY,{"derivedFrom":makeQuery(id+"F1.opRevolve","SWEPT_BODY",BODY,{"disambiguationData":[OSD([sQuery(id+"F0.wireOp",EDGE,"E1")])]}),"instanceName":"1"}),"instanceName":"1"}),"instanceName":"1"}),"instanceName":"1"}),"instanceName":"1"}),"instanceName":"1"}),"instanceName":"1"}),"instanceName":"1"}),"instanceName":"1"});
            var Q1337;
            Q1337=makeQuery(id+"F12.opPattern","COPY",BODY,{"derivedFrom":makeQuery(id+"F11.opPattern","COPY",BODY,{"derivedFrom":makeQuery(id+"F9.opPattern","COPY",BODY,{"derivedFrom":makeQuery(id+"F8.opPattern","COPY",BODY,{"derivedFrom":makeQuery(id+"F7.opPattern","COPY",BODY,{"derivedFrom":makeQuery(id+"F6.opPattern","COPY",BODY,{"derivedFrom":makeQuery(id+"F5.opPattern","COPY",BODY,{"derivedFrom":makeQuery(id+"F1.opRevolve","SWEPT_BODY",BODY,{"disambiguationData":[OSD([sQuery(id+"F0.wireOp",EDGE,"E1")])]}),"instanceName":"1"}),"instanceName":"1"}),"instanceName":"1"}),"instanceName":"1"}),"instanceName":"1"}),"instanceName":"1"}),"instanceName":"1"});
            var Q1338;
            Q1338=makeQuery(id+"F12.opPattern","COPY",BODY,{"derivedFrom":makeQuery(id+"F11.opPattern","COPY",BODY,{"derivedFrom":makeQuery(id+"F9.opPattern","COPY",BODY,{"derivedFrom":makeQuery(id+"F8.opPattern","COPY",BODY,{"derivedFrom":makeQuery(id+"F7.opPattern","COPY",BODY,{"derivedFrom":makeQuery(id+"F6.opPattern","COPY",BODY,{"derivedFrom":makeQuery(id+"F5.opPattern","COPY",BODY,{"derivedFrom":makeQuery(id+"F2.opPattern","COPY",BODY,{"derivedFrom":makeQuery(id+"F1.opRevolve","SWEPT_BODY",BODY,{"disambiguationData":[OSD([sQuery(id+"F0.wireOp",EDGE,"E1")])]}),"instanceName":"1"}),"instanceName":"1"}),"instanceName":"1"}),"instanceName":"1"}),"instanceName":"1"}),"instanceName":"1"}),"instanceName":"1"}),"instanceName":"1"});
            var Q1339;
            Q1339=makeQuery(id+"F12.opPattern","COPY",BODY,{"derivedFrom":makeQuery(id+"F11.opPattern","COPY",BODY,{"derivedFrom":makeQuery(id+"F9.opPattern","COPY",BODY,{"derivedFrom":makeQuery(id+"F8.opPattern","COPY",BODY,{"derivedFrom":makeQuery(id+"F7.opPattern","COPY",BODY,{"derivedFrom":makeQuery(id+"F6.opPattern","COPY",BODY,{"derivedFrom":makeQuery(id+"F5.opPattern","COPY",BODY,{"derivedFrom":makeQuery(id+"F3.opPattern","COPY",BODY,{"derivedFrom":makeQuery(id+"F2.opPattern","COPY",BODY,{"derivedFrom":makeQuery(id+"F1.opRevolve","SWEPT_BODY",BODY,{"disambiguationData":[OSD([sQuery(id+"F0.wireOp",EDGE,"E1")])]}),"instanceName":"1"}),"instanceName":"1"}),"instanceName":"1"}),"instanceName":"1"}),"instanceName":"1"}),"instanceName":"1"}),"instanceName":"1"}),"instanceName":"1"}),"instanceName":"1"});
            var Q1340;
            Q1340=makeQuery(id+"F12.opPattern","COPY",BODY,{"derivedFrom":makeQuery(id+"F11.opPattern","COPY",BODY,{"derivedFrom":makeQuery(id+"F9.opPattern","COPY",BODY,{"derivedFrom":makeQuery(id+"F8.opPattern","COPY",BODY,{"derivedFrom":makeQuery(id+"F7.opPattern","COPY",BODY,{"derivedFrom":makeQuery(id+"F6.opPattern","COPY",BODY,{"derivedFrom":makeQuery(id+"F5.opPattern","COPY",BODY,{"derivedFrom":makeQuery(id+"F4.opPattern","COPY",BODY,{"derivedFrom":makeQuery(id+"F1.opRevolve","SWEPT_BODY",BODY,{"disambiguationData":[OSD([sQuery(id+"F0.wireOp",EDGE,"E1")])]}),"instanceName":"1"}),"instanceName":"1"}),"instanceName":"1"}),"instanceName":"1"}),"instanceName":"1"}),"instanceName":"1"}),"instanceName":"1"}),"instanceName":"1"});
            var Q1341;
            Q1341=makeQuery(id+"F12.opPattern","COPY",BODY,{"derivedFrom":makeQuery(id+"F11.opPattern","COPY",BODY,{"derivedFrom":makeQuery(id+"F9.opPattern","COPY",BODY,{"derivedFrom":makeQuery(id+"F8.opPattern","COPY",BODY,{"derivedFrom":makeQuery(id+"F7.opPattern","COPY",BODY,{"derivedFrom":makeQuery(id+"F6.opPattern","COPY",BODY,{"derivedFrom":makeQuery(id+"F5.opPattern","COPY",BODY,{"derivedFrom":makeQuery(id+"F4.opPattern","COPY",BODY,{"derivedFrom":makeQuery(id+"F2.opPattern","COPY",BODY,{"derivedFrom":makeQuery(id+"F1.opRevolve","SWEPT_BODY",BODY,{"disambiguationData":[OSD([sQuery(id+"F0.wireOp",EDGE,"E1")])]}),"instanceName":"1"}),"instanceName":"1"}),"instanceName":"1"}),"instanceName":"1"}),"instanceName":"1"}),"instanceName":"1"}),"instanceName":"1"}),"instanceName":"1"}),"instanceName":"1"});
            var Q1342;
            Q1342=makeQuery(id+"F12.opPattern","COPY",BODY,{"derivedFrom":makeQuery(id+"F11.opPattern","COPY",BODY,{"derivedFrom":makeQuery(id+"F9.opPattern","COPY",BODY,{"derivedFrom":makeQuery(id+"F8.opPattern","COPY",BODY,{"derivedFrom":makeQuery(id+"F7.opPattern","COPY",BODY,{"derivedFrom":makeQuery(id+"F6.opPattern","COPY",BODY,{"derivedFrom":makeQuery(id+"F5.opPattern","COPY",BODY,{"derivedFrom":makeQuery(id+"F4.opPattern","COPY",BODY,{"derivedFrom":makeQuery(id+"F3.opPattern","COPY",BODY,{"derivedFrom":makeQuery(id+"F2.opPattern","COPY",BODY,{"derivedFrom":makeQuery(id+"F1.opRevolve","SWEPT_BODY",BODY,{"disambiguationData":[OSD([sQuery(id+"F0.wireOp",EDGE,"E1")])]}),"instanceName":"1"}),"instanceName":"1"}),"instanceName":"1"}),"instanceName":"1"}),"instanceName":"1"}),"instanceName":"1"}),"instanceName":"1"}),"instanceName":"1"}),"instanceName":"1"}),"instanceName":"1"});
            var Q1343;
            Q1343=makeQuery(id+"F12.opPattern","COPY",BODY,{"derivedFrom":makeQuery(id+"F11.opPattern","COPY",BODY,{"derivedFrom":makeQuery(id+"F10.opPattern","COPY",BODY,{"derivedFrom":makeQuery(id+"F1.opRevolve","SWEPT_BODY",BODY,{"disambiguationData":[OSD([sQuery(id+"F0.wireOp",EDGE,"E1")])]}),"instanceName":"1"}),"instanceName":"1"}),"instanceName":"1"});
            var Q1344;
            Q1344=makeQuery(id+"F12.opPattern","COPY",BODY,{"derivedFrom":makeQuery(id+"F11.opPattern","COPY",BODY,{"derivedFrom":makeQuery(id+"F10.opPattern","COPY",BODY,{"derivedFrom":makeQuery(id+"F2.opPattern","COPY",BODY,{"derivedFrom":makeQuery(id+"F1.opRevolve","SWEPT_BODY",BODY,{"disambiguationData":[OSD([sQuery(id+"F0.wireOp",EDGE,"E1")])]}),"instanceName":"1"}),"instanceName":"1"}),"instanceName":"1"}),"instanceName":"1"});
            var Q1345;
            Q1345=makeQuery(id+"F12.opPattern","COPY",BODY,{"derivedFrom":makeQuery(id+"F11.opPattern","COPY",BODY,{"derivedFrom":makeQuery(id+"F10.opPattern","COPY",BODY,{"derivedFrom":makeQuery(id+"F3.opPattern","COPY",BODY,{"derivedFrom":makeQuery(id+"F2.opPattern","COPY",BODY,{"derivedFrom":makeQuery(id+"F1.opRevolve","SWEPT_BODY",BODY,{"disambiguationData":[OSD([sQuery(id+"F0.wireOp",EDGE,"E1")])]}),"instanceName":"1"}),"instanceName":"1"}),"instanceName":"1"}),"instanceName":"1"}),"instanceName":"1"});
            var Q1346;
            Q1346=makeQuery(id+"F12.opPattern","COPY",BODY,{"derivedFrom":makeQuery(id+"F11.opPattern","COPY",BODY,{"derivedFrom":makeQuery(id+"F10.opPattern","COPY",BODY,{"derivedFrom":makeQuery(id+"F4.opPattern","COPY",BODY,{"derivedFrom":makeQuery(id+"F1.opRevolve","SWEPT_BODY",BODY,{"disambiguationData":[OSD([sQuery(id+"F0.wireOp",EDGE,"E1")])]}),"instanceName":"1"}),"instanceName":"1"}),"instanceName":"1"}),"instanceName":"1"});
            var Q1347;
            Q1347=makeQuery(id+"F12.opPattern","COPY",BODY,{"derivedFrom":makeQuery(id+"F11.opPattern","COPY",BODY,{"derivedFrom":makeQuery(id+"F10.opPattern","COPY",BODY,{"derivedFrom":makeQuery(id+"F4.opPattern","COPY",BODY,{"derivedFrom":makeQuery(id+"F2.opPattern","COPY",BODY,{"derivedFrom":makeQuery(id+"F1.opRevolve","SWEPT_BODY",BODY,{"disambiguationData":[OSD([sQuery(id+"F0.wireOp",EDGE,"E1")])]}),"instanceName":"1"}),"instanceName":"1"}),"instanceName":"1"}),"instanceName":"1"}),"instanceName":"1"});
            var Q1348;
            Q1348=makeQuery(id+"F12.opPattern","COPY",BODY,{"derivedFrom":makeQuery(id+"F11.opPattern","COPY",BODY,{"derivedFrom":makeQuery(id+"F10.opPattern","COPY",BODY,{"derivedFrom":makeQuery(id+"F4.opPattern","COPY",BODY,{"derivedFrom":makeQuery(id+"F3.opPattern","COPY",BODY,{"derivedFrom":makeQuery(id+"F2.opPattern","COPY",BODY,{"derivedFrom":makeQuery(id+"F1.opRevolve","SWEPT_BODY",BODY,{"disambiguationData":[OSD([sQuery(id+"F0.wireOp",EDGE,"E1")])]}),"instanceName":"1"}),"instanceName":"1"}),"instanceName":"1"}),"instanceName":"1"}),"instanceName":"1"}),"instanceName":"1"});
            var Q1349;
            Q1349=makeQuery(id+"F12.opPattern","COPY",BODY,{"derivedFrom":makeQuery(id+"F11.opPattern","COPY",BODY,{"derivedFrom":makeQuery(id+"F10.opPattern","COPY",BODY,{"derivedFrom":makeQuery(id+"F5.opPattern","COPY",BODY,{"derivedFrom":makeQuery(id+"F1.opRevolve","SWEPT_BODY",BODY,{"disambiguationData":[OSD([sQuery(id+"F0.wireOp",EDGE,"E1")])]}),"instanceName":"1"}),"instanceName":"1"}),"instanceName":"1"}),"instanceName":"1"});
            var Q1350;
            Q1350=makeQuery(id+"F12.opPattern","COPY",BODY,{"derivedFrom":makeQuery(id+"F11.opPattern","COPY",BODY,{"derivedFrom":makeQuery(id+"F10.opPattern","COPY",BODY,{"derivedFrom":makeQuery(id+"F5.opPattern","COPY",BODY,{"derivedFrom":makeQuery(id+"F2.opPattern","COPY",BODY,{"derivedFrom":makeQuery(id+"F1.opRevolve","SWEPT_BODY",BODY,{"disambiguationData":[OSD([sQuery(id+"F0.wireOp",EDGE,"E1")])]}),"instanceName":"1"}),"instanceName":"1"}),"instanceName":"1"}),"instanceName":"1"}),"instanceName":"1"});
            var Q1351;
            Q1351=makeQuery(id+"F12.opPattern","COPY",BODY,{"derivedFrom":makeQuery(id+"F11.opPattern","COPY",BODY,{"derivedFrom":makeQuery(id+"F10.opPattern","COPY",BODY,{"derivedFrom":makeQuery(id+"F5.opPattern","COPY",BODY,{"derivedFrom":makeQuery(id+"F3.opPattern","COPY",BODY,{"derivedFrom":makeQuery(id+"F2.opPattern","COPY",BODY,{"derivedFrom":makeQuery(id+"F1.opRevolve","SWEPT_BODY",BODY,{"disambiguationData":[OSD([sQuery(id+"F0.wireOp",EDGE,"E1")])]}),"instanceName":"1"}),"instanceName":"1"}),"instanceName":"1"}),"instanceName":"1"}),"instanceName":"1"}),"instanceName":"1"});
            var Q1352;
            Q1352=makeQuery(id+"F12.opPattern","COPY",BODY,{"derivedFrom":makeQuery(id+"F11.opPattern","COPY",BODY,{"derivedFrom":makeQuery(id+"F10.opPattern","COPY",BODY,{"derivedFrom":makeQuery(id+"F5.opPattern","COPY",BODY,{"derivedFrom":makeQuery(id+"F4.opPattern","COPY",BODY,{"derivedFrom":makeQuery(id+"F1.opRevolve","SWEPT_BODY",BODY,{"disambiguationData":[OSD([sQuery(id+"F0.wireOp",EDGE,"E1")])]}),"instanceName":"1"}),"instanceName":"1"}),"instanceName":"1"}),"instanceName":"1"}),"instanceName":"1"});
            var Q1353;
            Q1353=makeQuery(id+"F12.opPattern","COPY",BODY,{"derivedFrom":makeQuery(id+"F11.opPattern","COPY",BODY,{"derivedFrom":makeQuery(id+"F10.opPattern","COPY",BODY,{"derivedFrom":makeQuery(id+"F5.opPattern","COPY",BODY,{"derivedFrom":makeQuery(id+"F4.opPattern","COPY",BODY,{"derivedFrom":makeQuery(id+"F2.opPattern","COPY",BODY,{"derivedFrom":makeQuery(id+"F1.opRevolve","SWEPT_BODY",BODY,{"disambiguationData":[OSD([sQuery(id+"F0.wireOp",EDGE,"E1")])]}),"instanceName":"1"}),"instanceName":"1"}),"instanceName":"1"}),"instanceName":"1"}),"instanceName":"1"}),"instanceName":"1"});
            var Q1354;
            Q1354=makeQuery(id+"F12.opPattern","COPY",BODY,{"derivedFrom":makeQuery(id+"F11.opPattern","COPY",BODY,{"derivedFrom":makeQuery(id+"F10.opPattern","COPY",BODY,{"derivedFrom":makeQuery(id+"F5.opPattern","COPY",BODY,{"derivedFrom":makeQuery(id+"F4.opPattern","COPY",BODY,{"derivedFrom":makeQuery(id+"F3.opPattern","COPY",BODY,{"derivedFrom":makeQuery(id+"F2.opPattern","COPY",BODY,{"derivedFrom":makeQuery(id+"F1.opRevolve","SWEPT_BODY",BODY,{"disambiguationData":[OSD([sQuery(id+"F0.wireOp",EDGE,"E1")])]}),"instanceName":"1"}),"instanceName":"1"}),"instanceName":"1"}),"instanceName":"1"}),"instanceName":"1"}),"instanceName":"1"}),"instanceName":"1"});
            var Q1355;
            Q1355=makeQuery(id+"F12.opPattern","COPY",BODY,{"derivedFrom":makeQuery(id+"F11.opPattern","COPY",BODY,{"derivedFrom":makeQuery(id+"F10.opPattern","COPY",BODY,{"derivedFrom":makeQuery(id+"F6.opPattern","COPY",BODY,{"derivedFrom":makeQuery(id+"F1.opRevolve","SWEPT_BODY",BODY,{"disambiguationData":[OSD([sQuery(id+"F0.wireOp",EDGE,"E1")])]}),"instanceName":"1"}),"instanceName":"1"}),"instanceName":"1"}),"instanceName":"1"});
            var Q1356;
            Q1356=makeQuery(id+"F12.opPattern","COPY",BODY,{"derivedFrom":makeQuery(id+"F11.opPattern","COPY",BODY,{"derivedFrom":makeQuery(id+"F10.opPattern","COPY",BODY,{"derivedFrom":makeQuery(id+"F6.opPattern","COPY",BODY,{"derivedFrom":makeQuery(id+"F2.opPattern","COPY",BODY,{"derivedFrom":makeQuery(id+"F1.opRevolve","SWEPT_BODY",BODY,{"disambiguationData":[OSD([sQuery(id+"F0.wireOp",EDGE,"E1")])]}),"instanceName":"1"}),"instanceName":"1"}),"instanceName":"1"}),"instanceName":"1"}),"instanceName":"1"});
            var Q1357;
            Q1357=makeQuery(id+"F12.opPattern","COPY",BODY,{"derivedFrom":makeQuery(id+"F11.opPattern","COPY",BODY,{"derivedFrom":makeQuery(id+"F10.opPattern","COPY",BODY,{"derivedFrom":makeQuery(id+"F6.opPattern","COPY",BODY,{"derivedFrom":makeQuery(id+"F3.opPattern","COPY",BODY,{"derivedFrom":makeQuery(id+"F2.opPattern","COPY",BODY,{"derivedFrom":makeQuery(id+"F1.opRevolve","SWEPT_BODY",BODY,{"disambiguationData":[OSD([sQuery(id+"F0.wireOp",EDGE,"E1")])]}),"instanceName":"1"}),"instanceName":"1"}),"instanceName":"1"}),"instanceName":"1"}),"instanceName":"1"}),"instanceName":"1"});
            var Q1358;
            Q1358=makeQuery(id+"F12.opPattern","COPY",BODY,{"derivedFrom":makeQuery(id+"F11.opPattern","COPY",BODY,{"derivedFrom":makeQuery(id+"F10.opPattern","COPY",BODY,{"derivedFrom":makeQuery(id+"F6.opPattern","COPY",BODY,{"derivedFrom":makeQuery(id+"F4.opPattern","COPY",BODY,{"derivedFrom":makeQuery(id+"F1.opRevolve","SWEPT_BODY",BODY,{"disambiguationData":[OSD([sQuery(id+"F0.wireOp",EDGE,"E1")])]}),"instanceName":"1"}),"instanceName":"1"}),"instanceName":"1"}),"instanceName":"1"}),"instanceName":"1"});
            var Q1359;
            Q1359=makeQuery(id+"F12.opPattern","COPY",BODY,{"derivedFrom":makeQuery(id+"F11.opPattern","COPY",BODY,{"derivedFrom":makeQuery(id+"F10.opPattern","COPY",BODY,{"derivedFrom":makeQuery(id+"F6.opPattern","COPY",BODY,{"derivedFrom":makeQuery(id+"F4.opPattern","COPY",BODY,{"derivedFrom":makeQuery(id+"F2.opPattern","COPY",BODY,{"derivedFrom":makeQuery(id+"F1.opRevolve","SWEPT_BODY",BODY,{"disambiguationData":[OSD([sQuery(id+"F0.wireOp",EDGE,"E1")])]}),"instanceName":"1"}),"instanceName":"1"}),"instanceName":"1"}),"instanceName":"1"}),"instanceName":"1"}),"instanceName":"1"});
            var Q1360;
            Q1360=makeQuery(id+"F12.opPattern","COPY",BODY,{"derivedFrom":makeQuery(id+"F11.opPattern","COPY",BODY,{"derivedFrom":makeQuery(id+"F10.opPattern","COPY",BODY,{"derivedFrom":makeQuery(id+"F6.opPattern","COPY",BODY,{"derivedFrom":makeQuery(id+"F4.opPattern","COPY",BODY,{"derivedFrom":makeQuery(id+"F3.opPattern","COPY",BODY,{"derivedFrom":makeQuery(id+"F2.opPattern","COPY",BODY,{"derivedFrom":makeQuery(id+"F1.opRevolve","SWEPT_BODY",BODY,{"disambiguationData":[OSD([sQuery(id+"F0.wireOp",EDGE,"E1")])]}),"instanceName":"1"}),"instanceName":"1"}),"instanceName":"1"}),"instanceName":"1"}),"instanceName":"1"}),"instanceName":"1"}),"instanceName":"1"});
            var Q1361;
            Q1361=makeQuery(id+"F12.opPattern","COPY",BODY,{"derivedFrom":makeQuery(id+"F11.opPattern","COPY",BODY,{"derivedFrom":makeQuery(id+"F10.opPattern","COPY",BODY,{"derivedFrom":makeQuery(id+"F6.opPattern","COPY",BODY,{"derivedFrom":makeQuery(id+"F5.opPattern","COPY",BODY,{"derivedFrom":makeQuery(id+"F1.opRevolve","SWEPT_BODY",BODY,{"disambiguationData":[OSD([sQuery(id+"F0.wireOp",EDGE,"E1")])]}),"instanceName":"1"}),"instanceName":"1"}),"instanceName":"1"}),"instanceName":"1"}),"instanceName":"1"});
            var Q1362;
            Q1362=makeQuery(id+"F12.opPattern","COPY",BODY,{"derivedFrom":makeQuery(id+"F11.opPattern","COPY",BODY,{"derivedFrom":makeQuery(id+"F10.opPattern","COPY",BODY,{"derivedFrom":makeQuery(id+"F6.opPattern","COPY",BODY,{"derivedFrom":makeQuery(id+"F5.opPattern","COPY",BODY,{"derivedFrom":makeQuery(id+"F2.opPattern","COPY",BODY,{"derivedFrom":makeQuery(id+"F1.opRevolve","SWEPT_BODY",BODY,{"disambiguationData":[OSD([sQuery(id+"F0.wireOp",EDGE,"E1")])]}),"instanceName":"1"}),"instanceName":"1"}),"instanceName":"1"}),"instanceName":"1"}),"instanceName":"1"}),"instanceName":"1"});
            var Q1363;
            Q1363=makeQuery(id+"F12.opPattern","COPY",BODY,{"derivedFrom":makeQuery(id+"F11.opPattern","COPY",BODY,{"derivedFrom":makeQuery(id+"F10.opPattern","COPY",BODY,{"derivedFrom":makeQuery(id+"F6.opPattern","COPY",BODY,{"derivedFrom":makeQuery(id+"F5.opPattern","COPY",BODY,{"derivedFrom":makeQuery(id+"F3.opPattern","COPY",BODY,{"derivedFrom":makeQuery(id+"F2.opPattern","COPY",BODY,{"derivedFrom":makeQuery(id+"F1.opRevolve","SWEPT_BODY",BODY,{"disambiguationData":[OSD([sQuery(id+"F0.wireOp",EDGE,"E1")])]}),"instanceName":"1"}),"instanceName":"1"}),"instanceName":"1"}),"instanceName":"1"}),"instanceName":"1"}),"instanceName":"1"}),"instanceName":"1"});
            var Q1364;
            Q1364=makeQuery(id+"F12.opPattern","COPY",BODY,{"derivedFrom":makeQuery(id+"F11.opPattern","COPY",BODY,{"derivedFrom":makeQuery(id+"F10.opPattern","COPY",BODY,{"derivedFrom":makeQuery(id+"F6.opPattern","COPY",BODY,{"derivedFrom":makeQuery(id+"F5.opPattern","COPY",BODY,{"derivedFrom":makeQuery(id+"F4.opPattern","COPY",BODY,{"derivedFrom":makeQuery(id+"F1.opRevolve","SWEPT_BODY",BODY,{"disambiguationData":[OSD([sQuery(id+"F0.wireOp",EDGE,"E1")])]}),"instanceName":"1"}),"instanceName":"1"}),"instanceName":"1"}),"instanceName":"1"}),"instanceName":"1"}),"instanceName":"1"});
            var Q1365;
            Q1365=makeQuery(id+"F12.opPattern","COPY",BODY,{"derivedFrom":makeQuery(id+"F11.opPattern","COPY",BODY,{"derivedFrom":makeQuery(id+"F10.opPattern","COPY",BODY,{"derivedFrom":makeQuery(id+"F6.opPattern","COPY",BODY,{"derivedFrom":makeQuery(id+"F5.opPattern","COPY",BODY,{"derivedFrom":makeQuery(id+"F4.opPattern","COPY",BODY,{"derivedFrom":makeQuery(id+"F2.opPattern","COPY",BODY,{"derivedFrom":makeQuery(id+"F1.opRevolve","SWEPT_BODY",BODY,{"disambiguationData":[OSD([sQuery(id+"F0.wireOp",EDGE,"E1")])]}),"instanceName":"1"}),"instanceName":"1"}),"instanceName":"1"}),"instanceName":"1"}),"instanceName":"1"}),"instanceName":"1"}),"instanceName":"1"});
            var Q1366;
            Q1366=makeQuery(id+"F12.opPattern","COPY",BODY,{"derivedFrom":makeQuery(id+"F11.opPattern","COPY",BODY,{"derivedFrom":makeQuery(id+"F10.opPattern","COPY",BODY,{"derivedFrom":makeQuery(id+"F6.opPattern","COPY",BODY,{"derivedFrom":makeQuery(id+"F5.opPattern","COPY",BODY,{"derivedFrom":makeQuery(id+"F4.opPattern","COPY",BODY,{"derivedFrom":makeQuery(id+"F3.opPattern","COPY",BODY,{"derivedFrom":makeQuery(id+"F2.opPattern","COPY",BODY,{"derivedFrom":makeQuery(id+"F1.opRevolve","SWEPT_BODY",BODY,{"disambiguationData":[OSD([sQuery(id+"F0.wireOp",EDGE,"E1")])]}),"instanceName":"1"}),"instanceName":"1"}),"instanceName":"1"}),"instanceName":"1"}),"instanceName":"1"}),"instanceName":"1"}),"instanceName":"1"}),"instanceName":"1"});
            var Q1367;
            Q1367=makeQuery(id+"F12.opPattern","COPY",BODY,{"derivedFrom":makeQuery(id+"F11.opPattern","COPY",BODY,{"derivedFrom":makeQuery(id+"F10.opPattern","COPY",BODY,{"derivedFrom":makeQuery(id+"F7.opPattern","COPY",BODY,{"derivedFrom":makeQuery(id+"F1.opRevolve","SWEPT_BODY",BODY,{"disambiguationData":[OSD([sQuery(id+"F0.wireOp",EDGE,"E1")])]}),"instanceName":"1"}),"instanceName":"1"}),"instanceName":"1"}),"instanceName":"1"});
            var Q1368;
            Q1368=makeQuery(id+"F12.opPattern","COPY",BODY,{"derivedFrom":makeQuery(id+"F11.opPattern","COPY",BODY,{"derivedFrom":makeQuery(id+"F10.opPattern","COPY",BODY,{"derivedFrom":makeQuery(id+"F7.opPattern","COPY",BODY,{"derivedFrom":makeQuery(id+"F2.opPattern","COPY",BODY,{"derivedFrom":makeQuery(id+"F1.opRevolve","SWEPT_BODY",BODY,{"disambiguationData":[OSD([sQuery(id+"F0.wireOp",EDGE,"E1")])]}),"instanceName":"1"}),"instanceName":"1"}),"instanceName":"1"}),"instanceName":"1"}),"instanceName":"1"});
            var Q1369;
            Q1369=makeQuery(id+"F12.opPattern","COPY",BODY,{"derivedFrom":makeQuery(id+"F11.opPattern","COPY",BODY,{"derivedFrom":makeQuery(id+"F10.opPattern","COPY",BODY,{"derivedFrom":makeQuery(id+"F7.opPattern","COPY",BODY,{"derivedFrom":makeQuery(id+"F3.opPattern","COPY",BODY,{"derivedFrom":makeQuery(id+"F2.opPattern","COPY",BODY,{"derivedFrom":makeQuery(id+"F1.opRevolve","SWEPT_BODY",BODY,{"disambiguationData":[OSD([sQuery(id+"F0.wireOp",EDGE,"E1")])]}),"instanceName":"1"}),"instanceName":"1"}),"instanceName":"1"}),"instanceName":"1"}),"instanceName":"1"}),"instanceName":"1"});
            var Q1370;
            Q1370=makeQuery(id+"F12.opPattern","COPY",BODY,{"derivedFrom":makeQuery(id+"F11.opPattern","COPY",BODY,{"derivedFrom":makeQuery(id+"F10.opPattern","COPY",BODY,{"derivedFrom":makeQuery(id+"F7.opPattern","COPY",BODY,{"derivedFrom":makeQuery(id+"F4.opPattern","COPY",BODY,{"derivedFrom":makeQuery(id+"F1.opRevolve","SWEPT_BODY",BODY,{"disambiguationData":[OSD([sQuery(id+"F0.wireOp",EDGE,"E1")])]}),"instanceName":"1"}),"instanceName":"1"}),"instanceName":"1"}),"instanceName":"1"}),"instanceName":"1"});
            var Q1371;
            Q1371=makeQuery(id+"F12.opPattern","COPY",BODY,{"derivedFrom":makeQuery(id+"F11.opPattern","COPY",BODY,{"derivedFrom":makeQuery(id+"F10.opPattern","COPY",BODY,{"derivedFrom":makeQuery(id+"F7.opPattern","COPY",BODY,{"derivedFrom":makeQuery(id+"F4.opPattern","COPY",BODY,{"derivedFrom":makeQuery(id+"F2.opPattern","COPY",BODY,{"derivedFrom":makeQuery(id+"F1.opRevolve","SWEPT_BODY",BODY,{"disambiguationData":[OSD([sQuery(id+"F0.wireOp",EDGE,"E1")])]}),"instanceName":"1"}),"instanceName":"1"}),"instanceName":"1"}),"instanceName":"1"}),"instanceName":"1"}),"instanceName":"1"});
            var Q1372;
            Q1372=makeQuery(id+"F12.opPattern","COPY",BODY,{"derivedFrom":makeQuery(id+"F11.opPattern","COPY",BODY,{"derivedFrom":makeQuery(id+"F10.opPattern","COPY",BODY,{"derivedFrom":makeQuery(id+"F7.opPattern","COPY",BODY,{"derivedFrom":makeQuery(id+"F4.opPattern","COPY",BODY,{"derivedFrom":makeQuery(id+"F3.opPattern","COPY",BODY,{"derivedFrom":makeQuery(id+"F2.opPattern","COPY",BODY,{"derivedFrom":makeQuery(id+"F1.opRevolve","SWEPT_BODY",BODY,{"disambiguationData":[OSD([sQuery(id+"F0.wireOp",EDGE,"E1")])]}),"instanceName":"1"}),"instanceName":"1"}),"instanceName":"1"}),"instanceName":"1"}),"instanceName":"1"}),"instanceName":"1"}),"instanceName":"1"});
            var Q1373;
            Q1373=makeQuery(id+"F12.opPattern","COPY",BODY,{"derivedFrom":makeQuery(id+"F11.opPattern","COPY",BODY,{"derivedFrom":makeQuery(id+"F10.opPattern","COPY",BODY,{"derivedFrom":makeQuery(id+"F7.opPattern","COPY",BODY,{"derivedFrom":makeQuery(id+"F5.opPattern","COPY",BODY,{"derivedFrom":makeQuery(id+"F1.opRevolve","SWEPT_BODY",BODY,{"disambiguationData":[OSD([sQuery(id+"F0.wireOp",EDGE,"E1")])]}),"instanceName":"1"}),"instanceName":"1"}),"instanceName":"1"}),"instanceName":"1"}),"instanceName":"1"});
            var Q1374;
            Q1374=makeQuery(id+"F12.opPattern","COPY",BODY,{"derivedFrom":makeQuery(id+"F11.opPattern","COPY",BODY,{"derivedFrom":makeQuery(id+"F10.opPattern","COPY",BODY,{"derivedFrom":makeQuery(id+"F7.opPattern","COPY",BODY,{"derivedFrom":makeQuery(id+"F5.opPattern","COPY",BODY,{"derivedFrom":makeQuery(id+"F2.opPattern","COPY",BODY,{"derivedFrom":makeQuery(id+"F1.opRevolve","SWEPT_BODY",BODY,{"disambiguationData":[OSD([sQuery(id+"F0.wireOp",EDGE,"E1")])]}),"instanceName":"1"}),"instanceName":"1"}),"instanceName":"1"}),"instanceName":"1"}),"instanceName":"1"}),"instanceName":"1"});
            var Q1375;
            Q1375=makeQuery(id+"F12.opPattern","COPY",BODY,{"derivedFrom":makeQuery(id+"F11.opPattern","COPY",BODY,{"derivedFrom":makeQuery(id+"F10.opPattern","COPY",BODY,{"derivedFrom":makeQuery(id+"F7.opPattern","COPY",BODY,{"derivedFrom":makeQuery(id+"F5.opPattern","COPY",BODY,{"derivedFrom":makeQuery(id+"F3.opPattern","COPY",BODY,{"derivedFrom":makeQuery(id+"F2.opPattern","COPY",BODY,{"derivedFrom":makeQuery(id+"F1.opRevolve","SWEPT_BODY",BODY,{"disambiguationData":[OSD([sQuery(id+"F0.wireOp",EDGE,"E1")])]}),"instanceName":"1"}),"instanceName":"1"}),"instanceName":"1"}),"instanceName":"1"}),"instanceName":"1"}),"instanceName":"1"}),"instanceName":"1"});
            var Q1376;
            Q1376=makeQuery(id+"F12.opPattern","COPY",BODY,{"derivedFrom":makeQuery(id+"F11.opPattern","COPY",BODY,{"derivedFrom":makeQuery(id+"F10.opPattern","COPY",BODY,{"derivedFrom":makeQuery(id+"F7.opPattern","COPY",BODY,{"derivedFrom":makeQuery(id+"F5.opPattern","COPY",BODY,{"derivedFrom":makeQuery(id+"F4.opPattern","COPY",BODY,{"derivedFrom":makeQuery(id+"F1.opRevolve","SWEPT_BODY",BODY,{"disambiguationData":[OSD([sQuery(id+"F0.wireOp",EDGE,"E1")])]}),"instanceName":"1"}),"instanceName":"1"}),"instanceName":"1"}),"instanceName":"1"}),"instanceName":"1"}),"instanceName":"1"});
            var Q1377;
            Q1377=makeQuery(id+"F12.opPattern","COPY",BODY,{"derivedFrom":makeQuery(id+"F11.opPattern","COPY",BODY,{"derivedFrom":makeQuery(id+"F10.opPattern","COPY",BODY,{"derivedFrom":makeQuery(id+"F7.opPattern","COPY",BODY,{"derivedFrom":makeQuery(id+"F5.opPattern","COPY",BODY,{"derivedFrom":makeQuery(id+"F4.opPattern","COPY",BODY,{"derivedFrom":makeQuery(id+"F2.opPattern","COPY",BODY,{"derivedFrom":makeQuery(id+"F1.opRevolve","SWEPT_BODY",BODY,{"disambiguationData":[OSD([sQuery(id+"F0.wireOp",EDGE,"E1")])]}),"instanceName":"1"}),"instanceName":"1"}),"instanceName":"1"}),"instanceName":"1"}),"instanceName":"1"}),"instanceName":"1"}),"instanceName":"1"});
            var Q1378;
            Q1378=makeQuery(id+"F12.opPattern","COPY",BODY,{"derivedFrom":makeQuery(id+"F11.opPattern","COPY",BODY,{"derivedFrom":makeQuery(id+"F10.opPattern","COPY",BODY,{"derivedFrom":makeQuery(id+"F7.opPattern","COPY",BODY,{"derivedFrom":makeQuery(id+"F5.opPattern","COPY",BODY,{"derivedFrom":makeQuery(id+"F4.opPattern","COPY",BODY,{"derivedFrom":makeQuery(id+"F3.opPattern","COPY",BODY,{"derivedFrom":makeQuery(id+"F2.opPattern","COPY",BODY,{"derivedFrom":makeQuery(id+"F1.opRevolve","SWEPT_BODY",BODY,{"disambiguationData":[OSD([sQuery(id+"F0.wireOp",EDGE,"E1")])]}),"instanceName":"1"}),"instanceName":"1"}),"instanceName":"1"}),"instanceName":"1"}),"instanceName":"1"}),"instanceName":"1"}),"instanceName":"1"}),"instanceName":"1"});
            var Q1379;
            Q1379=makeQuery(id+"F12.opPattern","COPY",BODY,{"derivedFrom":makeQuery(id+"F11.opPattern","COPY",BODY,{"derivedFrom":makeQuery(id+"F10.opPattern","COPY",BODY,{"derivedFrom":makeQuery(id+"F7.opPattern","COPY",BODY,{"derivedFrom":makeQuery(id+"F6.opPattern","COPY",BODY,{"derivedFrom":makeQuery(id+"F1.opRevolve","SWEPT_BODY",BODY,{"disambiguationData":[OSD([sQuery(id+"F0.wireOp",EDGE,"E1")])]}),"instanceName":"1"}),"instanceName":"1"}),"instanceName":"1"}),"instanceName":"1"}),"instanceName":"1"});
            var Q1380;
            Q1380=makeQuery(id+"F12.opPattern","COPY",BODY,{"derivedFrom":makeQuery(id+"F11.opPattern","COPY",BODY,{"derivedFrom":makeQuery(id+"F10.opPattern","COPY",BODY,{"derivedFrom":makeQuery(id+"F7.opPattern","COPY",BODY,{"derivedFrom":makeQuery(id+"F6.opPattern","COPY",BODY,{"derivedFrom":makeQuery(id+"F2.opPattern","COPY",BODY,{"derivedFrom":makeQuery(id+"F1.opRevolve","SWEPT_BODY",BODY,{"disambiguationData":[OSD([sQuery(id+"F0.wireOp",EDGE,"E1")])]}),"instanceName":"1"}),"instanceName":"1"}),"instanceName":"1"}),"instanceName":"1"}),"instanceName":"1"}),"instanceName":"1"});
            var Q1381;
            Q1381=makeQuery(id+"F12.opPattern","COPY",BODY,{"derivedFrom":makeQuery(id+"F11.opPattern","COPY",BODY,{"derivedFrom":makeQuery(id+"F10.opPattern","COPY",BODY,{"derivedFrom":makeQuery(id+"F7.opPattern","COPY",BODY,{"derivedFrom":makeQuery(id+"F6.opPattern","COPY",BODY,{"derivedFrom":makeQuery(id+"F3.opPattern","COPY",BODY,{"derivedFrom":makeQuery(id+"F2.opPattern","COPY",BODY,{"derivedFrom":makeQuery(id+"F1.opRevolve","SWEPT_BODY",BODY,{"disambiguationData":[OSD([sQuery(id+"F0.wireOp",EDGE,"E1")])]}),"instanceName":"1"}),"instanceName":"1"}),"instanceName":"1"}),"instanceName":"1"}),"instanceName":"1"}),"instanceName":"1"}),"instanceName":"1"});
            var Q1382;
            Q1382=makeQuery(id+"F12.opPattern","COPY",BODY,{"derivedFrom":makeQuery(id+"F11.opPattern","COPY",BODY,{"derivedFrom":makeQuery(id+"F10.opPattern","COPY",BODY,{"derivedFrom":makeQuery(id+"F7.opPattern","COPY",BODY,{"derivedFrom":makeQuery(id+"F6.opPattern","COPY",BODY,{"derivedFrom":makeQuery(id+"F4.opPattern","COPY",BODY,{"derivedFrom":makeQuery(id+"F1.opRevolve","SWEPT_BODY",BODY,{"disambiguationData":[OSD([sQuery(id+"F0.wireOp",EDGE,"E1")])]}),"instanceName":"1"}),"instanceName":"1"}),"instanceName":"1"}),"instanceName":"1"}),"instanceName":"1"}),"instanceName":"1"});
            var Q1383;
            Q1383=makeQuery(id+"F12.opPattern","COPY",BODY,{"derivedFrom":makeQuery(id+"F11.opPattern","COPY",BODY,{"derivedFrom":makeQuery(id+"F10.opPattern","COPY",BODY,{"derivedFrom":makeQuery(id+"F7.opPattern","COPY",BODY,{"derivedFrom":makeQuery(id+"F6.opPattern","COPY",BODY,{"derivedFrom":makeQuery(id+"F4.opPattern","COPY",BODY,{"derivedFrom":makeQuery(id+"F2.opPattern","COPY",BODY,{"derivedFrom":makeQuery(id+"F1.opRevolve","SWEPT_BODY",BODY,{"disambiguationData":[OSD([sQuery(id+"F0.wireOp",EDGE,"E1")])]}),"instanceName":"1"}),"instanceName":"1"}),"instanceName":"1"}),"instanceName":"1"}),"instanceName":"1"}),"instanceName":"1"}),"instanceName":"1"});
            var Q1384;
            Q1384=makeQuery(id+"F12.opPattern","COPY",BODY,{"derivedFrom":makeQuery(id+"F11.opPattern","COPY",BODY,{"derivedFrom":makeQuery(id+"F10.opPattern","COPY",BODY,{"derivedFrom":makeQuery(id+"F7.opPattern","COPY",BODY,{"derivedFrom":makeQuery(id+"F6.opPattern","COPY",BODY,{"derivedFrom":makeQuery(id+"F4.opPattern","COPY",BODY,{"derivedFrom":makeQuery(id+"F3.opPattern","COPY",BODY,{"derivedFrom":makeQuery(id+"F2.opPattern","COPY",BODY,{"derivedFrom":makeQuery(id+"F1.opRevolve","SWEPT_BODY",BODY,{"disambiguationData":[OSD([sQuery(id+"F0.wireOp",EDGE,"E1")])]}),"instanceName":"1"}),"instanceName":"1"}),"instanceName":"1"}),"instanceName":"1"}),"instanceName":"1"}),"instanceName":"1"}),"instanceName":"1"}),"instanceName":"1"});
            var Q1385;
            Q1385=makeQuery(id+"F12.opPattern","COPY",BODY,{"derivedFrom":makeQuery(id+"F11.opPattern","COPY",BODY,{"derivedFrom":makeQuery(id+"F10.opPattern","COPY",BODY,{"derivedFrom":makeQuery(id+"F7.opPattern","COPY",BODY,{"derivedFrom":makeQuery(id+"F6.opPattern","COPY",BODY,{"derivedFrom":makeQuery(id+"F5.opPattern","COPY",BODY,{"derivedFrom":makeQuery(id+"F1.opRevolve","SWEPT_BODY",BODY,{"disambiguationData":[OSD([sQuery(id+"F0.wireOp",EDGE,"E1")])]}),"instanceName":"1"}),"instanceName":"1"}),"instanceName":"1"}),"instanceName":"1"}),"instanceName":"1"}),"instanceName":"1"});
            var Q1386;
            Q1386=makeQuery(id+"F12.opPattern","COPY",BODY,{"derivedFrom":makeQuery(id+"F11.opPattern","COPY",BODY,{"derivedFrom":makeQuery(id+"F10.opPattern","COPY",BODY,{"derivedFrom":makeQuery(id+"F7.opPattern","COPY",BODY,{"derivedFrom":makeQuery(id+"F6.opPattern","COPY",BODY,{"derivedFrom":makeQuery(id+"F5.opPattern","COPY",BODY,{"derivedFrom":makeQuery(id+"F2.opPattern","COPY",BODY,{"derivedFrom":makeQuery(id+"F1.opRevolve","SWEPT_BODY",BODY,{"disambiguationData":[OSD([sQuery(id+"F0.wireOp",EDGE,"E1")])]}),"instanceName":"1"}),"instanceName":"1"}),"instanceName":"1"}),"instanceName":"1"}),"instanceName":"1"}),"instanceName":"1"}),"instanceName":"1"});
            var Q1387;
            Q1387=makeQuery(id+"F12.opPattern","COPY",BODY,{"derivedFrom":makeQuery(id+"F11.opPattern","COPY",BODY,{"derivedFrom":makeQuery(id+"F10.opPattern","COPY",BODY,{"derivedFrom":makeQuery(id+"F7.opPattern","COPY",BODY,{"derivedFrom":makeQuery(id+"F6.opPattern","COPY",BODY,{"derivedFrom":makeQuery(id+"F5.opPattern","COPY",BODY,{"derivedFrom":makeQuery(id+"F3.opPattern","COPY",BODY,{"derivedFrom":makeQuery(id+"F2.opPattern","COPY",BODY,{"derivedFrom":makeQuery(id+"F1.opRevolve","SWEPT_BODY",BODY,{"disambiguationData":[OSD([sQuery(id+"F0.wireOp",EDGE,"E1")])]}),"instanceName":"1"}),"instanceName":"1"}),"instanceName":"1"}),"instanceName":"1"}),"instanceName":"1"}),"instanceName":"1"}),"instanceName":"1"}),"instanceName":"1"});
            var Q1388;
            Q1388=makeQuery(id+"F12.opPattern","COPY",BODY,{"derivedFrom":makeQuery(id+"F11.opPattern","COPY",BODY,{"derivedFrom":makeQuery(id+"F10.opPattern","COPY",BODY,{"derivedFrom":makeQuery(id+"F7.opPattern","COPY",BODY,{"derivedFrom":makeQuery(id+"F6.opPattern","COPY",BODY,{"derivedFrom":makeQuery(id+"F5.opPattern","COPY",BODY,{"derivedFrom":makeQuery(id+"F4.opPattern","COPY",BODY,{"derivedFrom":makeQuery(id+"F1.opRevolve","SWEPT_BODY",BODY,{"disambiguationData":[OSD([sQuery(id+"F0.wireOp",EDGE,"E1")])]}),"instanceName":"1"}),"instanceName":"1"}),"instanceName":"1"}),"instanceName":"1"}),"instanceName":"1"}),"instanceName":"1"}),"instanceName":"1"});
            var Q1389;
            Q1389=makeQuery(id+"F12.opPattern","COPY",BODY,{"derivedFrom":makeQuery(id+"F11.opPattern","COPY",BODY,{"derivedFrom":makeQuery(id+"F10.opPattern","COPY",BODY,{"derivedFrom":makeQuery(id+"F7.opPattern","COPY",BODY,{"derivedFrom":makeQuery(id+"F6.opPattern","COPY",BODY,{"derivedFrom":makeQuery(id+"F5.opPattern","COPY",BODY,{"derivedFrom":makeQuery(id+"F4.opPattern","COPY",BODY,{"derivedFrom":makeQuery(id+"F2.opPattern","COPY",BODY,{"derivedFrom":makeQuery(id+"F1.opRevolve","SWEPT_BODY",BODY,{"disambiguationData":[OSD([sQuery(id+"F0.wireOp",EDGE,"E1")])]}),"instanceName":"1"}),"instanceName":"1"}),"instanceName":"1"}),"instanceName":"1"}),"instanceName":"1"}),"instanceName":"1"}),"instanceName":"1"}),"instanceName":"1"});
            var Q1390;
            Q1390=makeQuery(id+"F12.opPattern","COPY",BODY,{"derivedFrom":makeQuery(id+"F11.opPattern","COPY",BODY,{"derivedFrom":makeQuery(id+"F10.opPattern","COPY",BODY,{"derivedFrom":makeQuery(id+"F7.opPattern","COPY",BODY,{"derivedFrom":makeQuery(id+"F6.opPattern","COPY",BODY,{"derivedFrom":makeQuery(id+"F5.opPattern","COPY",BODY,{"derivedFrom":makeQuery(id+"F4.opPattern","COPY",BODY,{"derivedFrom":makeQuery(id+"F3.opPattern","COPY",BODY,{"derivedFrom":makeQuery(id+"F2.opPattern","COPY",BODY,{"derivedFrom":makeQuery(id+"F1.opRevolve","SWEPT_BODY",BODY,{"disambiguationData":[OSD([sQuery(id+"F0.wireOp",EDGE,"E1")])]}),"instanceName":"1"}),"instanceName":"1"}),"instanceName":"1"}),"instanceName":"1"}),"instanceName":"1"}),"instanceName":"1"}),"instanceName":"1"}),"instanceName":"1"}),"instanceName":"1"});
            var Q1391;
            Q1391=makeQuery(id+"F12.opPattern","COPY",BODY,{"derivedFrom":makeQuery(id+"F11.opPattern","COPY",BODY,{"derivedFrom":makeQuery(id+"F10.opPattern","COPY",BODY,{"derivedFrom":makeQuery(id+"F8.opPattern","COPY",BODY,{"derivedFrom":makeQuery(id+"F1.opRevolve","SWEPT_BODY",BODY,{"disambiguationData":[OSD([sQuery(id+"F0.wireOp",EDGE,"E1")])]}),"instanceName":"1"}),"instanceName":"1"}),"instanceName":"1"}),"instanceName":"1"});
            var Q1392;
            Q1392=makeQuery(id+"F12.opPattern","COPY",BODY,{"derivedFrom":makeQuery(id+"F11.opPattern","COPY",BODY,{"derivedFrom":makeQuery(id+"F10.opPattern","COPY",BODY,{"derivedFrom":makeQuery(id+"F8.opPattern","COPY",BODY,{"derivedFrom":makeQuery(id+"F2.opPattern","COPY",BODY,{"derivedFrom":makeQuery(id+"F1.opRevolve","SWEPT_BODY",BODY,{"disambiguationData":[OSD([sQuery(id+"F0.wireOp",EDGE,"E1")])]}),"instanceName":"1"}),"instanceName":"1"}),"instanceName":"1"}),"instanceName":"1"}),"instanceName":"1"});
            var Q1393;
            Q1393=makeQuery(id+"F12.opPattern","COPY",BODY,{"derivedFrom":makeQuery(id+"F11.opPattern","COPY",BODY,{"derivedFrom":makeQuery(id+"F10.opPattern","COPY",BODY,{"derivedFrom":makeQuery(id+"F8.opPattern","COPY",BODY,{"derivedFrom":makeQuery(id+"F3.opPattern","COPY",BODY,{"derivedFrom":makeQuery(id+"F2.opPattern","COPY",BODY,{"derivedFrom":makeQuery(id+"F1.opRevolve","SWEPT_BODY",BODY,{"disambiguationData":[OSD([sQuery(id+"F0.wireOp",EDGE,"E1")])]}),"instanceName":"1"}),"instanceName":"1"}),"instanceName":"1"}),"instanceName":"1"}),"instanceName":"1"}),"instanceName":"1"});
            var Q1394;
            Q1394=makeQuery(id+"F12.opPattern","COPY",BODY,{"derivedFrom":makeQuery(id+"F11.opPattern","COPY",BODY,{"derivedFrom":makeQuery(id+"F10.opPattern","COPY",BODY,{"derivedFrom":makeQuery(id+"F8.opPattern","COPY",BODY,{"derivedFrom":makeQuery(id+"F4.opPattern","COPY",BODY,{"derivedFrom":makeQuery(id+"F1.opRevolve","SWEPT_BODY",BODY,{"disambiguationData":[OSD([sQuery(id+"F0.wireOp",EDGE,"E1")])]}),"instanceName":"1"}),"instanceName":"1"}),"instanceName":"1"}),"instanceName":"1"}),"instanceName":"1"});
            var Q1395;
            Q1395=makeQuery(id+"F12.opPattern","COPY",BODY,{"derivedFrom":makeQuery(id+"F11.opPattern","COPY",BODY,{"derivedFrom":makeQuery(id+"F10.opPattern","COPY",BODY,{"derivedFrom":makeQuery(id+"F8.opPattern","COPY",BODY,{"derivedFrom":makeQuery(id+"F4.opPattern","COPY",BODY,{"derivedFrom":makeQuery(id+"F2.opPattern","COPY",BODY,{"derivedFrom":makeQuery(id+"F1.opRevolve","SWEPT_BODY",BODY,{"disambiguationData":[OSD([sQuery(id+"F0.wireOp",EDGE,"E1")])]}),"instanceName":"1"}),"instanceName":"1"}),"instanceName":"1"}),"instanceName":"1"}),"instanceName":"1"}),"instanceName":"1"});
            var Q1396;
            Q1396=makeQuery(id+"F12.opPattern","COPY",BODY,{"derivedFrom":makeQuery(id+"F11.opPattern","COPY",BODY,{"derivedFrom":makeQuery(id+"F10.opPattern","COPY",BODY,{"derivedFrom":makeQuery(id+"F8.opPattern","COPY",BODY,{"derivedFrom":makeQuery(id+"F4.opPattern","COPY",BODY,{"derivedFrom":makeQuery(id+"F3.opPattern","COPY",BODY,{"derivedFrom":makeQuery(id+"F2.opPattern","COPY",BODY,{"derivedFrom":makeQuery(id+"F1.opRevolve","SWEPT_BODY",BODY,{"disambiguationData":[OSD([sQuery(id+"F0.wireOp",EDGE,"E1")])]}),"instanceName":"1"}),"instanceName":"1"}),"instanceName":"1"}),"instanceName":"1"}),"instanceName":"1"}),"instanceName":"1"}),"instanceName":"1"});
            var Q1397;
            Q1397=makeQuery(id+"F12.opPattern","COPY",BODY,{"derivedFrom":makeQuery(id+"F11.opPattern","COPY",BODY,{"derivedFrom":makeQuery(id+"F10.opPattern","COPY",BODY,{"derivedFrom":makeQuery(id+"F8.opPattern","COPY",BODY,{"derivedFrom":makeQuery(id+"F5.opPattern","COPY",BODY,{"derivedFrom":makeQuery(id+"F1.opRevolve","SWEPT_BODY",BODY,{"disambiguationData":[OSD([sQuery(id+"F0.wireOp",EDGE,"E1")])]}),"instanceName":"1"}),"instanceName":"1"}),"instanceName":"1"}),"instanceName":"1"}),"instanceName":"1"});
            var Q1398;
            Q1398=makeQuery(id+"F12.opPattern","COPY",BODY,{"derivedFrom":makeQuery(id+"F11.opPattern","COPY",BODY,{"derivedFrom":makeQuery(id+"F10.opPattern","COPY",BODY,{"derivedFrom":makeQuery(id+"F8.opPattern","COPY",BODY,{"derivedFrom":makeQuery(id+"F5.opPattern","COPY",BODY,{"derivedFrom":makeQuery(id+"F2.opPattern","COPY",BODY,{"derivedFrom":makeQuery(id+"F1.opRevolve","SWEPT_BODY",BODY,{"disambiguationData":[OSD([sQuery(id+"F0.wireOp",EDGE,"E1")])]}),"instanceName":"1"}),"instanceName":"1"}),"instanceName":"1"}),"instanceName":"1"}),"instanceName":"1"}),"instanceName":"1"});
            var Q1399;
            Q1399=makeQuery(id+"F12.opPattern","COPY",BODY,{"derivedFrom":makeQuery(id+"F11.opPattern","COPY",BODY,{"derivedFrom":makeQuery(id+"F10.opPattern","COPY",BODY,{"derivedFrom":makeQuery(id+"F8.opPattern","COPY",BODY,{"derivedFrom":makeQuery(id+"F5.opPattern","COPY",BODY,{"derivedFrom":makeQuery(id+"F3.opPattern","COPY",BODY,{"derivedFrom":makeQuery(id+"F2.opPattern","COPY",BODY,{"derivedFrom":makeQuery(id+"F1.opRevolve","SWEPT_BODY",BODY,{"disambiguationData":[OSD([sQuery(id+"F0.wireOp",EDGE,"E1")])]}),"instanceName":"1"}),"instanceName":"1"}),"instanceName":"1"}),"instanceName":"1"}),"instanceName":"1"}),"instanceName":"1"}),"instanceName":"1"});
            var Q1400;
            Q1400=makeQuery(id+"F12.opPattern","COPY",BODY,{"derivedFrom":makeQuery(id+"F11.opPattern","COPY",BODY,{"derivedFrom":makeQuery(id+"F10.opPattern","COPY",BODY,{"derivedFrom":makeQuery(id+"F8.opPattern","COPY",BODY,{"derivedFrom":makeQuery(id+"F5.opPattern","COPY",BODY,{"derivedFrom":makeQuery(id+"F4.opPattern","COPY",BODY,{"derivedFrom":makeQuery(id+"F1.opRevolve","SWEPT_BODY",BODY,{"disambiguationData":[OSD([sQuery(id+"F0.wireOp",EDGE,"E1")])]}),"instanceName":"1"}),"instanceName":"1"}),"instanceName":"1"}),"instanceName":"1"}),"instanceName":"1"}),"instanceName":"1"});
            var Q1401;
            Q1401=makeQuery(id+"F12.opPattern","COPY",BODY,{"derivedFrom":makeQuery(id+"F11.opPattern","COPY",BODY,{"derivedFrom":makeQuery(id+"F10.opPattern","COPY",BODY,{"derivedFrom":makeQuery(id+"F8.opPattern","COPY",BODY,{"derivedFrom":makeQuery(id+"F5.opPattern","COPY",BODY,{"derivedFrom":makeQuery(id+"F4.opPattern","COPY",BODY,{"derivedFrom":makeQuery(id+"F2.opPattern","COPY",BODY,{"derivedFrom":makeQuery(id+"F1.opRevolve","SWEPT_BODY",BODY,{"disambiguationData":[OSD([sQuery(id+"F0.wireOp",EDGE,"E1")])]}),"instanceName":"1"}),"instanceName":"1"}),"instanceName":"1"}),"instanceName":"1"}),"instanceName":"1"}),"instanceName":"1"}),"instanceName":"1"});
            var Q1402;
            Q1402=makeQuery(id+"F12.opPattern","COPY",BODY,{"derivedFrom":makeQuery(id+"F11.opPattern","COPY",BODY,{"derivedFrom":makeQuery(id+"F10.opPattern","COPY",BODY,{"derivedFrom":makeQuery(id+"F8.opPattern","COPY",BODY,{"derivedFrom":makeQuery(id+"F5.opPattern","COPY",BODY,{"derivedFrom":makeQuery(id+"F4.opPattern","COPY",BODY,{"derivedFrom":makeQuery(id+"F3.opPattern","COPY",BODY,{"derivedFrom":makeQuery(id+"F2.opPattern","COPY",BODY,{"derivedFrom":makeQuery(id+"F1.opRevolve","SWEPT_BODY",BODY,{"disambiguationData":[OSD([sQuery(id+"F0.wireOp",EDGE,"E1")])]}),"instanceName":"1"}),"instanceName":"1"}),"instanceName":"1"}),"instanceName":"1"}),"instanceName":"1"}),"instanceName":"1"}),"instanceName":"1"}),"instanceName":"1"});
            var Q1403;
            Q1403=makeQuery(id+"F12.opPattern","COPY",BODY,{"derivedFrom":makeQuery(id+"F11.opPattern","COPY",BODY,{"derivedFrom":makeQuery(id+"F10.opPattern","COPY",BODY,{"derivedFrom":makeQuery(id+"F8.opPattern","COPY",BODY,{"derivedFrom":makeQuery(id+"F6.opPattern","COPY",BODY,{"derivedFrom":makeQuery(id+"F1.opRevolve","SWEPT_BODY",BODY,{"disambiguationData":[OSD([sQuery(id+"F0.wireOp",EDGE,"E1")])]}),"instanceName":"1"}),"instanceName":"1"}),"instanceName":"1"}),"instanceName":"1"}),"instanceName":"1"});
            var Q1404;
            Q1404=makeQuery(id+"F12.opPattern","COPY",BODY,{"derivedFrom":makeQuery(id+"F11.opPattern","COPY",BODY,{"derivedFrom":makeQuery(id+"F10.opPattern","COPY",BODY,{"derivedFrom":makeQuery(id+"F8.opPattern","COPY",BODY,{"derivedFrom":makeQuery(id+"F6.opPattern","COPY",BODY,{"derivedFrom":makeQuery(id+"F2.opPattern","COPY",BODY,{"derivedFrom":makeQuery(id+"F1.opRevolve","SWEPT_BODY",BODY,{"disambiguationData":[OSD([sQuery(id+"F0.wireOp",EDGE,"E1")])]}),"instanceName":"1"}),"instanceName":"1"}),"instanceName":"1"}),"instanceName":"1"}),"instanceName":"1"}),"instanceName":"1"});
            var Q1405;
            Q1405=makeQuery(id+"F12.opPattern","COPY",BODY,{"derivedFrom":makeQuery(id+"F11.opPattern","COPY",BODY,{"derivedFrom":makeQuery(id+"F10.opPattern","COPY",BODY,{"derivedFrom":makeQuery(id+"F8.opPattern","COPY",BODY,{"derivedFrom":makeQuery(id+"F6.opPattern","COPY",BODY,{"derivedFrom":makeQuery(id+"F3.opPattern","COPY",BODY,{"derivedFrom":makeQuery(id+"F2.opPattern","COPY",BODY,{"derivedFrom":makeQuery(id+"F1.opRevolve","SWEPT_BODY",BODY,{"disambiguationData":[OSD([sQuery(id+"F0.wireOp",EDGE,"E1")])]}),"instanceName":"1"}),"instanceName":"1"}),"instanceName":"1"}),"instanceName":"1"}),"instanceName":"1"}),"instanceName":"1"}),"instanceName":"1"});
            var Q1406;
            Q1406=makeQuery(id+"F12.opPattern","COPY",BODY,{"derivedFrom":makeQuery(id+"F11.opPattern","COPY",BODY,{"derivedFrom":makeQuery(id+"F10.opPattern","COPY",BODY,{"derivedFrom":makeQuery(id+"F8.opPattern","COPY",BODY,{"derivedFrom":makeQuery(id+"F6.opPattern","COPY",BODY,{"derivedFrom":makeQuery(id+"F4.opPattern","COPY",BODY,{"derivedFrom":makeQuery(id+"F1.opRevolve","SWEPT_BODY",BODY,{"disambiguationData":[OSD([sQuery(id+"F0.wireOp",EDGE,"E1")])]}),"instanceName":"1"}),"instanceName":"1"}),"instanceName":"1"}),"instanceName":"1"}),"instanceName":"1"}),"instanceName":"1"});
            var Q1407;
            Q1407=makeQuery(id+"F12.opPattern","COPY",BODY,{"derivedFrom":makeQuery(id+"F11.opPattern","COPY",BODY,{"derivedFrom":makeQuery(id+"F10.opPattern","COPY",BODY,{"derivedFrom":makeQuery(id+"F8.opPattern","COPY",BODY,{"derivedFrom":makeQuery(id+"F6.opPattern","COPY",BODY,{"derivedFrom":makeQuery(id+"F4.opPattern","COPY",BODY,{"derivedFrom":makeQuery(id+"F2.opPattern","COPY",BODY,{"derivedFrom":makeQuery(id+"F1.opRevolve","SWEPT_BODY",BODY,{"disambiguationData":[OSD([sQuery(id+"F0.wireOp",EDGE,"E1")])]}),"instanceName":"1"}),"instanceName":"1"}),"instanceName":"1"}),"instanceName":"1"}),"instanceName":"1"}),"instanceName":"1"}),"instanceName":"1"});
            var Q1408;
            Q1408=makeQuery(id+"F12.opPattern","COPY",BODY,{"derivedFrom":makeQuery(id+"F11.opPattern","COPY",BODY,{"derivedFrom":makeQuery(id+"F10.opPattern","COPY",BODY,{"derivedFrom":makeQuery(id+"F8.opPattern","COPY",BODY,{"derivedFrom":makeQuery(id+"F6.opPattern","COPY",BODY,{"derivedFrom":makeQuery(id+"F4.opPattern","COPY",BODY,{"derivedFrom":makeQuery(id+"F3.opPattern","COPY",BODY,{"derivedFrom":makeQuery(id+"F2.opPattern","COPY",BODY,{"derivedFrom":makeQuery(id+"F1.opRevolve","SWEPT_BODY",BODY,{"disambiguationData":[OSD([sQuery(id+"F0.wireOp",EDGE,"E1")])]}),"instanceName":"1"}),"instanceName":"1"}),"instanceName":"1"}),"instanceName":"1"}),"instanceName":"1"}),"instanceName":"1"}),"instanceName":"1"}),"instanceName":"1"});
            var Q1409;
            Q1409=makeQuery(id+"F12.opPattern","COPY",BODY,{"derivedFrom":makeQuery(id+"F11.opPattern","COPY",BODY,{"derivedFrom":makeQuery(id+"F10.opPattern","COPY",BODY,{"derivedFrom":makeQuery(id+"F8.opPattern","COPY",BODY,{"derivedFrom":makeQuery(id+"F6.opPattern","COPY",BODY,{"derivedFrom":makeQuery(id+"F5.opPattern","COPY",BODY,{"derivedFrom":makeQuery(id+"F1.opRevolve","SWEPT_BODY",BODY,{"disambiguationData":[OSD([sQuery(id+"F0.wireOp",EDGE,"E1")])]}),"instanceName":"1"}),"instanceName":"1"}),"instanceName":"1"}),"instanceName":"1"}),"instanceName":"1"}),"instanceName":"1"});
            var Q1410;
            Q1410=makeQuery(id+"F12.opPattern","COPY",BODY,{"derivedFrom":makeQuery(id+"F11.opPattern","COPY",BODY,{"derivedFrom":makeQuery(id+"F10.opPattern","COPY",BODY,{"derivedFrom":makeQuery(id+"F8.opPattern","COPY",BODY,{"derivedFrom":makeQuery(id+"F6.opPattern","COPY",BODY,{"derivedFrom":makeQuery(id+"F5.opPattern","COPY",BODY,{"derivedFrom":makeQuery(id+"F2.opPattern","COPY",BODY,{"derivedFrom":makeQuery(id+"F1.opRevolve","SWEPT_BODY",BODY,{"disambiguationData":[OSD([sQuery(id+"F0.wireOp",EDGE,"E1")])]}),"instanceName":"1"}),"instanceName":"1"}),"instanceName":"1"}),"instanceName":"1"}),"instanceName":"1"}),"instanceName":"1"}),"instanceName":"1"});
            var Q1411;
            Q1411=makeQuery(id+"F12.opPattern","COPY",BODY,{"derivedFrom":makeQuery(id+"F11.opPattern","COPY",BODY,{"derivedFrom":makeQuery(id+"F10.opPattern","COPY",BODY,{"derivedFrom":makeQuery(id+"F8.opPattern","COPY",BODY,{"derivedFrom":makeQuery(id+"F6.opPattern","COPY",BODY,{"derivedFrom":makeQuery(id+"F5.opPattern","COPY",BODY,{"derivedFrom":makeQuery(id+"F3.opPattern","COPY",BODY,{"derivedFrom":makeQuery(id+"F2.opPattern","COPY",BODY,{"derivedFrom":makeQuery(id+"F1.opRevolve","SWEPT_BODY",BODY,{"disambiguationData":[OSD([sQuery(id+"F0.wireOp",EDGE,"E1")])]}),"instanceName":"1"}),"instanceName":"1"}),"instanceName":"1"}),"instanceName":"1"}),"instanceName":"1"}),"instanceName":"1"}),"instanceName":"1"}),"instanceName":"1"});
            var Q1412;
            Q1412=makeQuery(id+"F12.opPattern","COPY",BODY,{"derivedFrom":makeQuery(id+"F11.opPattern","COPY",BODY,{"derivedFrom":makeQuery(id+"F10.opPattern","COPY",BODY,{"derivedFrom":makeQuery(id+"F8.opPattern","COPY",BODY,{"derivedFrom":makeQuery(id+"F6.opPattern","COPY",BODY,{"derivedFrom":makeQuery(id+"F5.opPattern","COPY",BODY,{"derivedFrom":makeQuery(id+"F4.opPattern","COPY",BODY,{"derivedFrom":makeQuery(id+"F1.opRevolve","SWEPT_BODY",BODY,{"disambiguationData":[OSD([sQuery(id+"F0.wireOp",EDGE,"E1")])]}),"instanceName":"1"}),"instanceName":"1"}),"instanceName":"1"}),"instanceName":"1"}),"instanceName":"1"}),"instanceName":"1"}),"instanceName":"1"});
            var Q1413;
            Q1413=makeQuery(id+"F12.opPattern","COPY",BODY,{"derivedFrom":makeQuery(id+"F11.opPattern","COPY",BODY,{"derivedFrom":makeQuery(id+"F10.opPattern","COPY",BODY,{"derivedFrom":makeQuery(id+"F8.opPattern","COPY",BODY,{"derivedFrom":makeQuery(id+"F6.opPattern","COPY",BODY,{"derivedFrom":makeQuery(id+"F5.opPattern","COPY",BODY,{"derivedFrom":makeQuery(id+"F4.opPattern","COPY",BODY,{"derivedFrom":makeQuery(id+"F2.opPattern","COPY",BODY,{"derivedFrom":makeQuery(id+"F1.opRevolve","SWEPT_BODY",BODY,{"disambiguationData":[OSD([sQuery(id+"F0.wireOp",EDGE,"E1")])]}),"instanceName":"1"}),"instanceName":"1"}),"instanceName":"1"}),"instanceName":"1"}),"instanceName":"1"}),"instanceName":"1"}),"instanceName":"1"}),"instanceName":"1"});
            var Q1414;
            Q1414=makeQuery(id+"F12.opPattern","COPY",BODY,{"derivedFrom":makeQuery(id+"F11.opPattern","COPY",BODY,{"derivedFrom":makeQuery(id+"F10.opPattern","COPY",BODY,{"derivedFrom":makeQuery(id+"F8.opPattern","COPY",BODY,{"derivedFrom":makeQuery(id+"F6.opPattern","COPY",BODY,{"derivedFrom":makeQuery(id+"F5.opPattern","COPY",BODY,{"derivedFrom":makeQuery(id+"F4.opPattern","COPY",BODY,{"derivedFrom":makeQuery(id+"F3.opPattern","COPY",BODY,{"derivedFrom":makeQuery(id+"F2.opPattern","COPY",BODY,{"derivedFrom":makeQuery(id+"F1.opRevolve","SWEPT_BODY",BODY,{"disambiguationData":[OSD([sQuery(id+"F0.wireOp",EDGE,"E1")])]}),"instanceName":"1"}),"instanceName":"1"}),"instanceName":"1"}),"instanceName":"1"}),"instanceName":"1"}),"instanceName":"1"}),"instanceName":"1"}),"instanceName":"1"}),"instanceName":"1"});
            var Q1415;
            Q1415=makeQuery(id+"F12.opPattern","COPY",BODY,{"derivedFrom":makeQuery(id+"F11.opPattern","COPY",BODY,{"derivedFrom":makeQuery(id+"F10.opPattern","COPY",BODY,{"derivedFrom":makeQuery(id+"F8.opPattern","COPY",BODY,{"derivedFrom":makeQuery(id+"F7.opPattern","COPY",BODY,{"derivedFrom":makeQuery(id+"F1.opRevolve","SWEPT_BODY",BODY,{"disambiguationData":[OSD([sQuery(id+"F0.wireOp",EDGE,"E1")])]}),"instanceName":"1"}),"instanceName":"1"}),"instanceName":"1"}),"instanceName":"1"}),"instanceName":"1"});
            var Q1416;
            Q1416=makeQuery(id+"F12.opPattern","COPY",BODY,{"derivedFrom":makeQuery(id+"F11.opPattern","COPY",BODY,{"derivedFrom":makeQuery(id+"F10.opPattern","COPY",BODY,{"derivedFrom":makeQuery(id+"F8.opPattern","COPY",BODY,{"derivedFrom":makeQuery(id+"F7.opPattern","COPY",BODY,{"derivedFrom":makeQuery(id+"F2.opPattern","COPY",BODY,{"derivedFrom":makeQuery(id+"F1.opRevolve","SWEPT_BODY",BODY,{"disambiguationData":[OSD([sQuery(id+"F0.wireOp",EDGE,"E1")])]}),"instanceName":"1"}),"instanceName":"1"}),"instanceName":"1"}),"instanceName":"1"}),"instanceName":"1"}),"instanceName":"1"});
            var Q1417;
            Q1417=makeQuery(id+"F12.opPattern","COPY",BODY,{"derivedFrom":makeQuery(id+"F11.opPattern","COPY",BODY,{"derivedFrom":makeQuery(id+"F10.opPattern","COPY",BODY,{"derivedFrom":makeQuery(id+"F8.opPattern","COPY",BODY,{"derivedFrom":makeQuery(id+"F7.opPattern","COPY",BODY,{"derivedFrom":makeQuery(id+"F3.opPattern","COPY",BODY,{"derivedFrom":makeQuery(id+"F2.opPattern","COPY",BODY,{"derivedFrom":makeQuery(id+"F1.opRevolve","SWEPT_BODY",BODY,{"disambiguationData":[OSD([sQuery(id+"F0.wireOp",EDGE,"E1")])]}),"instanceName":"1"}),"instanceName":"1"}),"instanceName":"1"}),"instanceName":"1"}),"instanceName":"1"}),"instanceName":"1"}),"instanceName":"1"});
            var Q1418;
            Q1418=makeQuery(id+"F12.opPattern","COPY",BODY,{"derivedFrom":makeQuery(id+"F11.opPattern","COPY",BODY,{"derivedFrom":makeQuery(id+"F10.opPattern","COPY",BODY,{"derivedFrom":makeQuery(id+"F8.opPattern","COPY",BODY,{"derivedFrom":makeQuery(id+"F7.opPattern","COPY",BODY,{"derivedFrom":makeQuery(id+"F4.opPattern","COPY",BODY,{"derivedFrom":makeQuery(id+"F1.opRevolve","SWEPT_BODY",BODY,{"disambiguationData":[OSD([sQuery(id+"F0.wireOp",EDGE,"E1")])]}),"instanceName":"1"}),"instanceName":"1"}),"instanceName":"1"}),"instanceName":"1"}),"instanceName":"1"}),"instanceName":"1"});
            var Q1419;
            Q1419=makeQuery(id+"F12.opPattern","COPY",BODY,{"derivedFrom":makeQuery(id+"F11.opPattern","COPY",BODY,{"derivedFrom":makeQuery(id+"F10.opPattern","COPY",BODY,{"derivedFrom":makeQuery(id+"F8.opPattern","COPY",BODY,{"derivedFrom":makeQuery(id+"F7.opPattern","COPY",BODY,{"derivedFrom":makeQuery(id+"F4.opPattern","COPY",BODY,{"derivedFrom":makeQuery(id+"F2.opPattern","COPY",BODY,{"derivedFrom":makeQuery(id+"F1.opRevolve","SWEPT_BODY",BODY,{"disambiguationData":[OSD([sQuery(id+"F0.wireOp",EDGE,"E1")])]}),"instanceName":"1"}),"instanceName":"1"}),"instanceName":"1"}),"instanceName":"1"}),"instanceName":"1"}),"instanceName":"1"}),"instanceName":"1"});
            var Q1420;
            Q1420=makeQuery(id+"F12.opPattern","COPY",BODY,{"derivedFrom":makeQuery(id+"F11.opPattern","COPY",BODY,{"derivedFrom":makeQuery(id+"F10.opPattern","COPY",BODY,{"derivedFrom":makeQuery(id+"F8.opPattern","COPY",BODY,{"derivedFrom":makeQuery(id+"F7.opPattern","COPY",BODY,{"derivedFrom":makeQuery(id+"F4.opPattern","COPY",BODY,{"derivedFrom":makeQuery(id+"F3.opPattern","COPY",BODY,{"derivedFrom":makeQuery(id+"F2.opPattern","COPY",BODY,{"derivedFrom":makeQuery(id+"F1.opRevolve","SWEPT_BODY",BODY,{"disambiguationData":[OSD([sQuery(id+"F0.wireOp",EDGE,"E1")])]}),"instanceName":"1"}),"instanceName":"1"}),"instanceName":"1"}),"instanceName":"1"}),"instanceName":"1"}),"instanceName":"1"}),"instanceName":"1"}),"instanceName":"1"});
            var Q1421;
            Q1421=makeQuery(id+"F12.opPattern","COPY",BODY,{"derivedFrom":makeQuery(id+"F11.opPattern","COPY",BODY,{"derivedFrom":makeQuery(id+"F10.opPattern","COPY",BODY,{"derivedFrom":makeQuery(id+"F8.opPattern","COPY",BODY,{"derivedFrom":makeQuery(id+"F7.opPattern","COPY",BODY,{"derivedFrom":makeQuery(id+"F5.opPattern","COPY",BODY,{"derivedFrom":makeQuery(id+"F1.opRevolve","SWEPT_BODY",BODY,{"disambiguationData":[OSD([sQuery(id+"F0.wireOp",EDGE,"E1")])]}),"instanceName":"1"}),"instanceName":"1"}),"instanceName":"1"}),"instanceName":"1"}),"instanceName":"1"}),"instanceName":"1"});
            var Q1422;
            Q1422=makeQuery(id+"F12.opPattern","COPY",BODY,{"derivedFrom":makeQuery(id+"F11.opPattern","COPY",BODY,{"derivedFrom":makeQuery(id+"F10.opPattern","COPY",BODY,{"derivedFrom":makeQuery(id+"F8.opPattern","COPY",BODY,{"derivedFrom":makeQuery(id+"F7.opPattern","COPY",BODY,{"derivedFrom":makeQuery(id+"F5.opPattern","COPY",BODY,{"derivedFrom":makeQuery(id+"F2.opPattern","COPY",BODY,{"derivedFrom":makeQuery(id+"F1.opRevolve","SWEPT_BODY",BODY,{"disambiguationData":[OSD([sQuery(id+"F0.wireOp",EDGE,"E1")])]}),"instanceName":"1"}),"instanceName":"1"}),"instanceName":"1"}),"instanceName":"1"}),"instanceName":"1"}),"instanceName":"1"}),"instanceName":"1"});
            var Q1423;
            Q1423=makeQuery(id+"F12.opPattern","COPY",BODY,{"derivedFrom":makeQuery(id+"F11.opPattern","COPY",BODY,{"derivedFrom":makeQuery(id+"F10.opPattern","COPY",BODY,{"derivedFrom":makeQuery(id+"F8.opPattern","COPY",BODY,{"derivedFrom":makeQuery(id+"F7.opPattern","COPY",BODY,{"derivedFrom":makeQuery(id+"F5.opPattern","COPY",BODY,{"derivedFrom":makeQuery(id+"F3.opPattern","COPY",BODY,{"derivedFrom":makeQuery(id+"F2.opPattern","COPY",BODY,{"derivedFrom":makeQuery(id+"F1.opRevolve","SWEPT_BODY",BODY,{"disambiguationData":[OSD([sQuery(id+"F0.wireOp",EDGE,"E1")])]}),"instanceName":"1"}),"instanceName":"1"}),"instanceName":"1"}),"instanceName":"1"}),"instanceName":"1"}),"instanceName":"1"}),"instanceName":"1"}),"instanceName":"1"});
            var Q1424;
            Q1424=makeQuery(id+"F12.opPattern","COPY",BODY,{"derivedFrom":makeQuery(id+"F11.opPattern","COPY",BODY,{"derivedFrom":makeQuery(id+"F10.opPattern","COPY",BODY,{"derivedFrom":makeQuery(id+"F8.opPattern","COPY",BODY,{"derivedFrom":makeQuery(id+"F7.opPattern","COPY",BODY,{"derivedFrom":makeQuery(id+"F5.opPattern","COPY",BODY,{"derivedFrom":makeQuery(id+"F4.opPattern","COPY",BODY,{"derivedFrom":makeQuery(id+"F1.opRevolve","SWEPT_BODY",BODY,{"disambiguationData":[OSD([sQuery(id+"F0.wireOp",EDGE,"E1")])]}),"instanceName":"1"}),"instanceName":"1"}),"instanceName":"1"}),"instanceName":"1"}),"instanceName":"1"}),"instanceName":"1"}),"instanceName":"1"});
            var Q1425;
            Q1425=makeQuery(id+"F12.opPattern","COPY",BODY,{"derivedFrom":makeQuery(id+"F11.opPattern","COPY",BODY,{"derivedFrom":makeQuery(id+"F10.opPattern","COPY",BODY,{"derivedFrom":makeQuery(id+"F8.opPattern","COPY",BODY,{"derivedFrom":makeQuery(id+"F7.opPattern","COPY",BODY,{"derivedFrom":makeQuery(id+"F5.opPattern","COPY",BODY,{"derivedFrom":makeQuery(id+"F4.opPattern","COPY",BODY,{"derivedFrom":makeQuery(id+"F2.opPattern","COPY",BODY,{"derivedFrom":makeQuery(id+"F1.opRevolve","SWEPT_BODY",BODY,{"disambiguationData":[OSD([sQuery(id+"F0.wireOp",EDGE,"E1")])]}),"instanceName":"1"}),"instanceName":"1"}),"instanceName":"1"}),"instanceName":"1"}),"instanceName":"1"}),"instanceName":"1"}),"instanceName":"1"}),"instanceName":"1"});
            var Q1426;
            Q1426=makeQuery(id+"F12.opPattern","COPY",BODY,{"derivedFrom":makeQuery(id+"F11.opPattern","COPY",BODY,{"derivedFrom":makeQuery(id+"F10.opPattern","COPY",BODY,{"derivedFrom":makeQuery(id+"F8.opPattern","COPY",BODY,{"derivedFrom":makeQuery(id+"F7.opPattern","COPY",BODY,{"derivedFrom":makeQuery(id+"F5.opPattern","COPY",BODY,{"derivedFrom":makeQuery(id+"F4.opPattern","COPY",BODY,{"derivedFrom":makeQuery(id+"F3.opPattern","COPY",BODY,{"derivedFrom":makeQuery(id+"F2.opPattern","COPY",BODY,{"derivedFrom":makeQuery(id+"F1.opRevolve","SWEPT_BODY",BODY,{"disambiguationData":[OSD([sQuery(id+"F0.wireOp",EDGE,"E1")])]}),"instanceName":"1"}),"instanceName":"1"}),"instanceName":"1"}),"instanceName":"1"}),"instanceName":"1"}),"instanceName":"1"}),"instanceName":"1"}),"instanceName":"1"}),"instanceName":"1"});
            var Q1427;
            Q1427=makeQuery(id+"F12.opPattern","COPY",BODY,{"derivedFrom":makeQuery(id+"F11.opPattern","COPY",BODY,{"derivedFrom":makeQuery(id+"F10.opPattern","COPY",BODY,{"derivedFrom":makeQuery(id+"F8.opPattern","COPY",BODY,{"derivedFrom":makeQuery(id+"F7.opPattern","COPY",BODY,{"derivedFrom":makeQuery(id+"F6.opPattern","COPY",BODY,{"derivedFrom":makeQuery(id+"F1.opRevolve","SWEPT_BODY",BODY,{"disambiguationData":[OSD([sQuery(id+"F0.wireOp",EDGE,"E1")])]}),"instanceName":"1"}),"instanceName":"1"}),"instanceName":"1"}),"instanceName":"1"}),"instanceName":"1"}),"instanceName":"1"});
            var Q1428;
            Q1428=makeQuery(id+"F12.opPattern","COPY",BODY,{"derivedFrom":makeQuery(id+"F11.opPattern","COPY",BODY,{"derivedFrom":makeQuery(id+"F10.opPattern","COPY",BODY,{"derivedFrom":makeQuery(id+"F8.opPattern","COPY",BODY,{"derivedFrom":makeQuery(id+"F7.opPattern","COPY",BODY,{"derivedFrom":makeQuery(id+"F6.opPattern","COPY",BODY,{"derivedFrom":makeQuery(id+"F2.opPattern","COPY",BODY,{"derivedFrom":makeQuery(id+"F1.opRevolve","SWEPT_BODY",BODY,{"disambiguationData":[OSD([sQuery(id+"F0.wireOp",EDGE,"E1")])]}),"instanceName":"1"}),"instanceName":"1"}),"instanceName":"1"}),"instanceName":"1"}),"instanceName":"1"}),"instanceName":"1"}),"instanceName":"1"});
            var Q1429;
            Q1429=makeQuery(id+"F12.opPattern","COPY",BODY,{"derivedFrom":makeQuery(id+"F11.opPattern","COPY",BODY,{"derivedFrom":makeQuery(id+"F10.opPattern","COPY",BODY,{"derivedFrom":makeQuery(id+"F8.opPattern","COPY",BODY,{"derivedFrom":makeQuery(id+"F7.opPattern","COPY",BODY,{"derivedFrom":makeQuery(id+"F6.opPattern","COPY",BODY,{"derivedFrom":makeQuery(id+"F3.opPattern","COPY",BODY,{"derivedFrom":makeQuery(id+"F2.opPattern","COPY",BODY,{"derivedFrom":makeQuery(id+"F1.opRevolve","SWEPT_BODY",BODY,{"disambiguationData":[OSD([sQuery(id+"F0.wireOp",EDGE,"E1")])]}),"instanceName":"1"}),"instanceName":"1"}),"instanceName":"1"}),"instanceName":"1"}),"instanceName":"1"}),"instanceName":"1"}),"instanceName":"1"}),"instanceName":"1"});
            var Q1430;
            Q1430=makeQuery(id+"F12.opPattern","COPY",BODY,{"derivedFrom":makeQuery(id+"F11.opPattern","COPY",BODY,{"derivedFrom":makeQuery(id+"F10.opPattern","COPY",BODY,{"derivedFrom":makeQuery(id+"F8.opPattern","COPY",BODY,{"derivedFrom":makeQuery(id+"F7.opPattern","COPY",BODY,{"derivedFrom":makeQuery(id+"F6.opPattern","COPY",BODY,{"derivedFrom":makeQuery(id+"F4.opPattern","COPY",BODY,{"derivedFrom":makeQuery(id+"F1.opRevolve","SWEPT_BODY",BODY,{"disambiguationData":[OSD([sQuery(id+"F0.wireOp",EDGE,"E1")])]}),"instanceName":"1"}),"instanceName":"1"}),"instanceName":"1"}),"instanceName":"1"}),"instanceName":"1"}),"instanceName":"1"}),"instanceName":"1"});
            var Q1431;
            Q1431=makeQuery(id+"F12.opPattern","COPY",BODY,{"derivedFrom":makeQuery(id+"F11.opPattern","COPY",BODY,{"derivedFrom":makeQuery(id+"F10.opPattern","COPY",BODY,{"derivedFrom":makeQuery(id+"F8.opPattern","COPY",BODY,{"derivedFrom":makeQuery(id+"F7.opPattern","COPY",BODY,{"derivedFrom":makeQuery(id+"F6.opPattern","COPY",BODY,{"derivedFrom":makeQuery(id+"F4.opPattern","COPY",BODY,{"derivedFrom":makeQuery(id+"F2.opPattern","COPY",BODY,{"derivedFrom":makeQuery(id+"F1.opRevolve","SWEPT_BODY",BODY,{"disambiguationData":[OSD([sQuery(id+"F0.wireOp",EDGE,"E1")])]}),"instanceName":"1"}),"instanceName":"1"}),"instanceName":"1"}),"instanceName":"1"}),"instanceName":"1"}),"instanceName":"1"}),"instanceName":"1"}),"instanceName":"1"});
            var Q1432;
            Q1432=makeQuery(id+"F12.opPattern","COPY",BODY,{"derivedFrom":makeQuery(id+"F11.opPattern","COPY",BODY,{"derivedFrom":makeQuery(id+"F10.opPattern","COPY",BODY,{"derivedFrom":makeQuery(id+"F8.opPattern","COPY",BODY,{"derivedFrom":makeQuery(id+"F7.opPattern","COPY",BODY,{"derivedFrom":makeQuery(id+"F6.opPattern","COPY",BODY,{"derivedFrom":makeQuery(id+"F4.opPattern","COPY",BODY,{"derivedFrom":makeQuery(id+"F3.opPattern","COPY",BODY,{"derivedFrom":makeQuery(id+"F2.opPattern","COPY",BODY,{"derivedFrom":makeQuery(id+"F1.opRevolve","SWEPT_BODY",BODY,{"disambiguationData":[OSD([sQuery(id+"F0.wireOp",EDGE,"E1")])]}),"instanceName":"1"}),"instanceName":"1"}),"instanceName":"1"}),"instanceName":"1"}),"instanceName":"1"}),"instanceName":"1"}),"instanceName":"1"}),"instanceName":"1"}),"instanceName":"1"});
            var Q1433;
            Q1433=makeQuery(id+"F12.opPattern","COPY",BODY,{"derivedFrom":makeQuery(id+"F11.opPattern","COPY",BODY,{"derivedFrom":makeQuery(id+"F10.opPattern","COPY",BODY,{"derivedFrom":makeQuery(id+"F8.opPattern","COPY",BODY,{"derivedFrom":makeQuery(id+"F7.opPattern","COPY",BODY,{"derivedFrom":makeQuery(id+"F6.opPattern","COPY",BODY,{"derivedFrom":makeQuery(id+"F5.opPattern","COPY",BODY,{"derivedFrom":makeQuery(id+"F1.opRevolve","SWEPT_BODY",BODY,{"disambiguationData":[OSD([sQuery(id+"F0.wireOp",EDGE,"E1")])]}),"instanceName":"1"}),"instanceName":"1"}),"instanceName":"1"}),"instanceName":"1"}),"instanceName":"1"}),"instanceName":"1"}),"instanceName":"1"});
            var Q1434;
            Q1434=makeQuery(id+"F12.opPattern","COPY",BODY,{"derivedFrom":makeQuery(id+"F11.opPattern","COPY",BODY,{"derivedFrom":makeQuery(id+"F10.opPattern","COPY",BODY,{"derivedFrom":makeQuery(id+"F8.opPattern","COPY",BODY,{"derivedFrom":makeQuery(id+"F7.opPattern","COPY",BODY,{"derivedFrom":makeQuery(id+"F6.opPattern","COPY",BODY,{"derivedFrom":makeQuery(id+"F5.opPattern","COPY",BODY,{"derivedFrom":makeQuery(id+"F2.opPattern","COPY",BODY,{"derivedFrom":makeQuery(id+"F1.opRevolve","SWEPT_BODY",BODY,{"disambiguationData":[OSD([sQuery(id+"F0.wireOp",EDGE,"E1")])]}),"instanceName":"1"}),"instanceName":"1"}),"instanceName":"1"}),"instanceName":"1"}),"instanceName":"1"}),"instanceName":"1"}),"instanceName":"1"}),"instanceName":"1"});
            var Q1435;
            Q1435=makeQuery(id+"F12.opPattern","COPY",BODY,{"derivedFrom":makeQuery(id+"F11.opPattern","COPY",BODY,{"derivedFrom":makeQuery(id+"F10.opPattern","COPY",BODY,{"derivedFrom":makeQuery(id+"F8.opPattern","COPY",BODY,{"derivedFrom":makeQuery(id+"F7.opPattern","COPY",BODY,{"derivedFrom":makeQuery(id+"F6.opPattern","COPY",BODY,{"derivedFrom":makeQuery(id+"F5.opPattern","COPY",BODY,{"derivedFrom":makeQuery(id+"F3.opPattern","COPY",BODY,{"derivedFrom":makeQuery(id+"F2.opPattern","COPY",BODY,{"derivedFrom":makeQuery(id+"F1.opRevolve","SWEPT_BODY",BODY,{"disambiguationData":[OSD([sQuery(id+"F0.wireOp",EDGE,"E1")])]}),"instanceName":"1"}),"instanceName":"1"}),"instanceName":"1"}),"instanceName":"1"}),"instanceName":"1"}),"instanceName":"1"}),"instanceName":"1"}),"instanceName":"1"}),"instanceName":"1"});
            var Q1436;
            Q1436=makeQuery(id+"F12.opPattern","COPY",BODY,{"derivedFrom":makeQuery(id+"F11.opPattern","COPY",BODY,{"derivedFrom":makeQuery(id+"F10.opPattern","COPY",BODY,{"derivedFrom":makeQuery(id+"F8.opPattern","COPY",BODY,{"derivedFrom":makeQuery(id+"F7.opPattern","COPY",BODY,{"derivedFrom":makeQuery(id+"F6.opPattern","COPY",BODY,{"derivedFrom":makeQuery(id+"F5.opPattern","COPY",BODY,{"derivedFrom":makeQuery(id+"F4.opPattern","COPY",BODY,{"derivedFrom":makeQuery(id+"F1.opRevolve","SWEPT_BODY",BODY,{"disambiguationData":[OSD([sQuery(id+"F0.wireOp",EDGE,"E1")])]}),"instanceName":"1"}),"instanceName":"1"}),"instanceName":"1"}),"instanceName":"1"}),"instanceName":"1"}),"instanceName":"1"}),"instanceName":"1"}),"instanceName":"1"});
            var Q1437;
            Q1437=makeQuery(id+"F12.opPattern","COPY",BODY,{"derivedFrom":makeQuery(id+"F11.opPattern","COPY",BODY,{"derivedFrom":makeQuery(id+"F10.opPattern","COPY",BODY,{"derivedFrom":makeQuery(id+"F8.opPattern","COPY",BODY,{"derivedFrom":makeQuery(id+"F7.opPattern","COPY",BODY,{"derivedFrom":makeQuery(id+"F6.opPattern","COPY",BODY,{"derivedFrom":makeQuery(id+"F5.opPattern","COPY",BODY,{"derivedFrom":makeQuery(id+"F4.opPattern","COPY",BODY,{"derivedFrom":makeQuery(id+"F2.opPattern","COPY",BODY,{"derivedFrom":makeQuery(id+"F1.opRevolve","SWEPT_BODY",BODY,{"disambiguationData":[OSD([sQuery(id+"F0.wireOp",EDGE,"E1")])]}),"instanceName":"1"}),"instanceName":"1"}),"instanceName":"1"}),"instanceName":"1"}),"instanceName":"1"}),"instanceName":"1"}),"instanceName":"1"}),"instanceName":"1"}),"instanceName":"1"});
            var Q1438;
            Q1438=makeQuery(id+"F12.opPattern","COPY",BODY,{"derivedFrom":makeQuery(id+"F11.opPattern","COPY",BODY,{"derivedFrom":makeQuery(id+"F10.opPattern","COPY",BODY,{"derivedFrom":makeQuery(id+"F8.opPattern","COPY",BODY,{"derivedFrom":makeQuery(id+"F7.opPattern","COPY",BODY,{"derivedFrom":makeQuery(id+"F6.opPattern","COPY",BODY,{"derivedFrom":makeQuery(id+"F5.opPattern","COPY",BODY,{"derivedFrom":makeQuery(id+"F4.opPattern","COPY",BODY,{"derivedFrom":makeQuery(id+"F3.opPattern","COPY",BODY,{"derivedFrom":makeQuery(id+"F2.opPattern","COPY",BODY,{"derivedFrom":makeQuery(id+"F1.opRevolve","SWEPT_BODY",BODY,{"disambiguationData":[OSD([sQuery(id+"F0.wireOp",EDGE,"E1")])]}),"instanceName":"1"}),"instanceName":"1"}),"instanceName":"1"}),"instanceName":"1"}),"instanceName":"1"}),"instanceName":"1"}),"instanceName":"1"}),"instanceName":"1"}),"instanceName":"1"}),"instanceName":"1"});
            var Q1439;
            Q1439=makeQuery(id+"F12.opPattern","COPY",BODY,{"derivedFrom":makeQuery(id+"F11.opPattern","COPY",BODY,{"derivedFrom":makeQuery(id+"F10.opPattern","COPY",BODY,{"derivedFrom":makeQuery(id+"F9.opPattern","COPY",BODY,{"derivedFrom":makeQuery(id+"F1.opRevolve","SWEPT_BODY",BODY,{"disambiguationData":[OSD([sQuery(id+"F0.wireOp",EDGE,"E1")])]}),"instanceName":"1"}),"instanceName":"1"}),"instanceName":"1"}),"instanceName":"1"});
            var Q1440;
            Q1440=makeQuery(id+"F12.opPattern","COPY",BODY,{"derivedFrom":makeQuery(id+"F11.opPattern","COPY",BODY,{"derivedFrom":makeQuery(id+"F10.opPattern","COPY",BODY,{"derivedFrom":makeQuery(id+"F9.opPattern","COPY",BODY,{"derivedFrom":makeQuery(id+"F2.opPattern","COPY",BODY,{"derivedFrom":makeQuery(id+"F1.opRevolve","SWEPT_BODY",BODY,{"disambiguationData":[OSD([sQuery(id+"F0.wireOp",EDGE,"E1")])]}),"instanceName":"1"}),"instanceName":"1"}),"instanceName":"1"}),"instanceName":"1"}),"instanceName":"1"});
            var Q1441;
            Q1441=makeQuery(id+"F12.opPattern","COPY",BODY,{"derivedFrom":makeQuery(id+"F11.opPattern","COPY",BODY,{"derivedFrom":makeQuery(id+"F10.opPattern","COPY",BODY,{"derivedFrom":makeQuery(id+"F9.opPattern","COPY",BODY,{"derivedFrom":makeQuery(id+"F3.opPattern","COPY",BODY,{"derivedFrom":makeQuery(id+"F2.opPattern","COPY",BODY,{"derivedFrom":makeQuery(id+"F1.opRevolve","SWEPT_BODY",BODY,{"disambiguationData":[OSD([sQuery(id+"F0.wireOp",EDGE,"E1")])]}),"instanceName":"1"}),"instanceName":"1"}),"instanceName":"1"}),"instanceName":"1"}),"instanceName":"1"}),"instanceName":"1"});
            var Q1442;
            Q1442=makeQuery(id+"F12.opPattern","COPY",BODY,{"derivedFrom":makeQuery(id+"F11.opPattern","COPY",BODY,{"derivedFrom":makeQuery(id+"F10.opPattern","COPY",BODY,{"derivedFrom":makeQuery(id+"F9.opPattern","COPY",BODY,{"derivedFrom":makeQuery(id+"F4.opPattern","COPY",BODY,{"derivedFrom":makeQuery(id+"F1.opRevolve","SWEPT_BODY",BODY,{"disambiguationData":[OSD([sQuery(id+"F0.wireOp",EDGE,"E1")])]}),"instanceName":"1"}),"instanceName":"1"}),"instanceName":"1"}),"instanceName":"1"}),"instanceName":"1"});
            var Q1443;
            Q1443=makeQuery(id+"F12.opPattern","COPY",BODY,{"derivedFrom":makeQuery(id+"F11.opPattern","COPY",BODY,{"derivedFrom":makeQuery(id+"F10.opPattern","COPY",BODY,{"derivedFrom":makeQuery(id+"F9.opPattern","COPY",BODY,{"derivedFrom":makeQuery(id+"F4.opPattern","COPY",BODY,{"derivedFrom":makeQuery(id+"F2.opPattern","COPY",BODY,{"derivedFrom":makeQuery(id+"F1.opRevolve","SWEPT_BODY",BODY,{"disambiguationData":[OSD([sQuery(id+"F0.wireOp",EDGE,"E1")])]}),"instanceName":"1"}),"instanceName":"1"}),"instanceName":"1"}),"instanceName":"1"}),"instanceName":"1"}),"instanceName":"1"});
            var Q1444;
            Q1444=makeQuery(id+"F12.opPattern","COPY",BODY,{"derivedFrom":makeQuery(id+"F11.opPattern","COPY",BODY,{"derivedFrom":makeQuery(id+"F10.opPattern","COPY",BODY,{"derivedFrom":makeQuery(id+"F9.opPattern","COPY",BODY,{"derivedFrom":makeQuery(id+"F4.opPattern","COPY",BODY,{"derivedFrom":makeQuery(id+"F3.opPattern","COPY",BODY,{"derivedFrom":makeQuery(id+"F2.opPattern","COPY",BODY,{"derivedFrom":makeQuery(id+"F1.opRevolve","SWEPT_BODY",BODY,{"disambiguationData":[OSD([sQuery(id+"F0.wireOp",EDGE,"E1")])]}),"instanceName":"1"}),"instanceName":"1"}),"instanceName":"1"}),"instanceName":"1"}),"instanceName":"1"}),"instanceName":"1"}),"instanceName":"1"});
            var Q1445;
            Q1445=makeQuery(id+"F12.opPattern","COPY",BODY,{"derivedFrom":makeQuery(id+"F11.opPattern","COPY",BODY,{"derivedFrom":makeQuery(id+"F10.opPattern","COPY",BODY,{"derivedFrom":makeQuery(id+"F9.opPattern","COPY",BODY,{"derivedFrom":makeQuery(id+"F5.opPattern","COPY",BODY,{"derivedFrom":makeQuery(id+"F1.opRevolve","SWEPT_BODY",BODY,{"disambiguationData":[OSD([sQuery(id+"F0.wireOp",EDGE,"E1")])]}),"instanceName":"1"}),"instanceName":"1"}),"instanceName":"1"}),"instanceName":"1"}),"instanceName":"1"});
            var Q1446;
            Q1446=makeQuery(id+"F12.opPattern","COPY",BODY,{"derivedFrom":makeQuery(id+"F11.opPattern","COPY",BODY,{"derivedFrom":makeQuery(id+"F10.opPattern","COPY",BODY,{"derivedFrom":makeQuery(id+"F9.opPattern","COPY",BODY,{"derivedFrom":makeQuery(id+"F5.opPattern","COPY",BODY,{"derivedFrom":makeQuery(id+"F2.opPattern","COPY",BODY,{"derivedFrom":makeQuery(id+"F1.opRevolve","SWEPT_BODY",BODY,{"disambiguationData":[OSD([sQuery(id+"F0.wireOp",EDGE,"E1")])]}),"instanceName":"1"}),"instanceName":"1"}),"instanceName":"1"}),"instanceName":"1"}),"instanceName":"1"}),"instanceName":"1"});
            var Q1447;
            Q1447=makeQuery(id+"F12.opPattern","COPY",BODY,{"derivedFrom":makeQuery(id+"F11.opPattern","COPY",BODY,{"derivedFrom":makeQuery(id+"F10.opPattern","COPY",BODY,{"derivedFrom":makeQuery(id+"F9.opPattern","COPY",BODY,{"derivedFrom":makeQuery(id+"F5.opPattern","COPY",BODY,{"derivedFrom":makeQuery(id+"F3.opPattern","COPY",BODY,{"derivedFrom":makeQuery(id+"F2.opPattern","COPY",BODY,{"derivedFrom":makeQuery(id+"F1.opRevolve","SWEPT_BODY",BODY,{"disambiguationData":[OSD([sQuery(id+"F0.wireOp",EDGE,"E1")])]}),"instanceName":"1"}),"instanceName":"1"}),"instanceName":"1"}),"instanceName":"1"}),"instanceName":"1"}),"instanceName":"1"}),"instanceName":"1"});
            var Q1448;
            Q1448=makeQuery(id+"F12.opPattern","COPY",BODY,{"derivedFrom":makeQuery(id+"F11.opPattern","COPY",BODY,{"derivedFrom":makeQuery(id+"F10.opPattern","COPY",BODY,{"derivedFrom":makeQuery(id+"F9.opPattern","COPY",BODY,{"derivedFrom":makeQuery(id+"F5.opPattern","COPY",BODY,{"derivedFrom":makeQuery(id+"F4.opPattern","COPY",BODY,{"derivedFrom":makeQuery(id+"F1.opRevolve","SWEPT_BODY",BODY,{"disambiguationData":[OSD([sQuery(id+"F0.wireOp",EDGE,"E1")])]}),"instanceName":"1"}),"instanceName":"1"}),"instanceName":"1"}),"instanceName":"1"}),"instanceName":"1"}),"instanceName":"1"});
            var Q1449;
            Q1449=makeQuery(id+"F12.opPattern","COPY",BODY,{"derivedFrom":makeQuery(id+"F11.opPattern","COPY",BODY,{"derivedFrom":makeQuery(id+"F10.opPattern","COPY",BODY,{"derivedFrom":makeQuery(id+"F9.opPattern","COPY",BODY,{"derivedFrom":makeQuery(id+"F5.opPattern","COPY",BODY,{"derivedFrom":makeQuery(id+"F4.opPattern","COPY",BODY,{"derivedFrom":makeQuery(id+"F2.opPattern","COPY",BODY,{"derivedFrom":makeQuery(id+"F1.opRevolve","SWEPT_BODY",BODY,{"disambiguationData":[OSD([sQuery(id+"F0.wireOp",EDGE,"E1")])]}),"instanceName":"1"}),"instanceName":"1"}),"instanceName":"1"}),"instanceName":"1"}),"instanceName":"1"}),"instanceName":"1"}),"instanceName":"1"});
            var Q1450;
            Q1450=makeQuery(id+"F12.opPattern","COPY",BODY,{"derivedFrom":makeQuery(id+"F11.opPattern","COPY",BODY,{"derivedFrom":makeQuery(id+"F10.opPattern","COPY",BODY,{"derivedFrom":makeQuery(id+"F9.opPattern","COPY",BODY,{"derivedFrom":makeQuery(id+"F5.opPattern","COPY",BODY,{"derivedFrom":makeQuery(id+"F4.opPattern","COPY",BODY,{"derivedFrom":makeQuery(id+"F3.opPattern","COPY",BODY,{"derivedFrom":makeQuery(id+"F2.opPattern","COPY",BODY,{"derivedFrom":makeQuery(id+"F1.opRevolve","SWEPT_BODY",BODY,{"disambiguationData":[OSD([sQuery(id+"F0.wireOp",EDGE,"E1")])]}),"instanceName":"1"}),"instanceName":"1"}),"instanceName":"1"}),"instanceName":"1"}),"instanceName":"1"}),"instanceName":"1"}),"instanceName":"1"}),"instanceName":"1"});
            var Q1451;
            Q1451=makeQuery(id+"F12.opPattern","COPY",BODY,{"derivedFrom":makeQuery(id+"F11.opPattern","COPY",BODY,{"derivedFrom":makeQuery(id+"F10.opPattern","COPY",BODY,{"derivedFrom":makeQuery(id+"F9.opPattern","COPY",BODY,{"derivedFrom":makeQuery(id+"F6.opPattern","COPY",BODY,{"derivedFrom":makeQuery(id+"F1.opRevolve","SWEPT_BODY",BODY,{"disambiguationData":[OSD([sQuery(id+"F0.wireOp",EDGE,"E1")])]}),"instanceName":"1"}),"instanceName":"1"}),"instanceName":"1"}),"instanceName":"1"}),"instanceName":"1"});
            var Q1452;
            Q1452=makeQuery(id+"F12.opPattern","COPY",BODY,{"derivedFrom":makeQuery(id+"F11.opPattern","COPY",BODY,{"derivedFrom":makeQuery(id+"F10.opPattern","COPY",BODY,{"derivedFrom":makeQuery(id+"F9.opPattern","COPY",BODY,{"derivedFrom":makeQuery(id+"F6.opPattern","COPY",BODY,{"derivedFrom":makeQuery(id+"F2.opPattern","COPY",BODY,{"derivedFrom":makeQuery(id+"F1.opRevolve","SWEPT_BODY",BODY,{"disambiguationData":[OSD([sQuery(id+"F0.wireOp",EDGE,"E1")])]}),"instanceName":"1"}),"instanceName":"1"}),"instanceName":"1"}),"instanceName":"1"}),"instanceName":"1"}),"instanceName":"1"});
            var Q1453;
            Q1453=makeQuery(id+"F12.opPattern","COPY",BODY,{"derivedFrom":makeQuery(id+"F11.opPattern","COPY",BODY,{"derivedFrom":makeQuery(id+"F10.opPattern","COPY",BODY,{"derivedFrom":makeQuery(id+"F9.opPattern","COPY",BODY,{"derivedFrom":makeQuery(id+"F6.opPattern","COPY",BODY,{"derivedFrom":makeQuery(id+"F3.opPattern","COPY",BODY,{"derivedFrom":makeQuery(id+"F2.opPattern","COPY",BODY,{"derivedFrom":makeQuery(id+"F1.opRevolve","SWEPT_BODY",BODY,{"disambiguationData":[OSD([sQuery(id+"F0.wireOp",EDGE,"E1")])]}),"instanceName":"1"}),"instanceName":"1"}),"instanceName":"1"}),"instanceName":"1"}),"instanceName":"1"}),"instanceName":"1"}),"instanceName":"1"});
            var Q1454;
            Q1454=makeQuery(id+"F12.opPattern","COPY",BODY,{"derivedFrom":makeQuery(id+"F11.opPattern","COPY",BODY,{"derivedFrom":makeQuery(id+"F10.opPattern","COPY",BODY,{"derivedFrom":makeQuery(id+"F9.opPattern","COPY",BODY,{"derivedFrom":makeQuery(id+"F6.opPattern","COPY",BODY,{"derivedFrom":makeQuery(id+"F4.opPattern","COPY",BODY,{"derivedFrom":makeQuery(id+"F1.opRevolve","SWEPT_BODY",BODY,{"disambiguationData":[OSD([sQuery(id+"F0.wireOp",EDGE,"E1")])]}),"instanceName":"1"}),"instanceName":"1"}),"instanceName":"1"}),"instanceName":"1"}),"instanceName":"1"}),"instanceName":"1"});
            var Q1455;
            Q1455=makeQuery(id+"F12.opPattern","COPY",BODY,{"derivedFrom":makeQuery(id+"F11.opPattern","COPY",BODY,{"derivedFrom":makeQuery(id+"F10.opPattern","COPY",BODY,{"derivedFrom":makeQuery(id+"F9.opPattern","COPY",BODY,{"derivedFrom":makeQuery(id+"F6.opPattern","COPY",BODY,{"derivedFrom":makeQuery(id+"F4.opPattern","COPY",BODY,{"derivedFrom":makeQuery(id+"F2.opPattern","COPY",BODY,{"derivedFrom":makeQuery(id+"F1.opRevolve","SWEPT_BODY",BODY,{"disambiguationData":[OSD([sQuery(id+"F0.wireOp",EDGE,"E1")])]}),"instanceName":"1"}),"instanceName":"1"}),"instanceName":"1"}),"instanceName":"1"}),"instanceName":"1"}),"instanceName":"1"}),"instanceName":"1"});
            var Q1456;
            Q1456=makeQuery(id+"F12.opPattern","COPY",BODY,{"derivedFrom":makeQuery(id+"F11.opPattern","COPY",BODY,{"derivedFrom":makeQuery(id+"F10.opPattern","COPY",BODY,{"derivedFrom":makeQuery(id+"F9.opPattern","COPY",BODY,{"derivedFrom":makeQuery(id+"F6.opPattern","COPY",BODY,{"derivedFrom":makeQuery(id+"F4.opPattern","COPY",BODY,{"derivedFrom":makeQuery(id+"F3.opPattern","COPY",BODY,{"derivedFrom":makeQuery(id+"F2.opPattern","COPY",BODY,{"derivedFrom":makeQuery(id+"F1.opRevolve","SWEPT_BODY",BODY,{"disambiguationData":[OSD([sQuery(id+"F0.wireOp",EDGE,"E1")])]}),"instanceName":"1"}),"instanceName":"1"}),"instanceName":"1"}),"instanceName":"1"}),"instanceName":"1"}),"instanceName":"1"}),"instanceName":"1"}),"instanceName":"1"});
            var Q1457;
            Q1457=makeQuery(id+"F12.opPattern","COPY",BODY,{"derivedFrom":makeQuery(id+"F11.opPattern","COPY",BODY,{"derivedFrom":makeQuery(id+"F10.opPattern","COPY",BODY,{"derivedFrom":makeQuery(id+"F9.opPattern","COPY",BODY,{"derivedFrom":makeQuery(id+"F6.opPattern","COPY",BODY,{"derivedFrom":makeQuery(id+"F5.opPattern","COPY",BODY,{"derivedFrom":makeQuery(id+"F1.opRevolve","SWEPT_BODY",BODY,{"disambiguationData":[OSD([sQuery(id+"F0.wireOp",EDGE,"E1")])]}),"instanceName":"1"}),"instanceName":"1"}),"instanceName":"1"}),"instanceName":"1"}),"instanceName":"1"}),"instanceName":"1"});
            var Q1458;
            Q1458=makeQuery(id+"F12.opPattern","COPY",BODY,{"derivedFrom":makeQuery(id+"F11.opPattern","COPY",BODY,{"derivedFrom":makeQuery(id+"F10.opPattern","COPY",BODY,{"derivedFrom":makeQuery(id+"F9.opPattern","COPY",BODY,{"derivedFrom":makeQuery(id+"F6.opPattern","COPY",BODY,{"derivedFrom":makeQuery(id+"F5.opPattern","COPY",BODY,{"derivedFrom":makeQuery(id+"F2.opPattern","COPY",BODY,{"derivedFrom":makeQuery(id+"F1.opRevolve","SWEPT_BODY",BODY,{"disambiguationData":[OSD([sQuery(id+"F0.wireOp",EDGE,"E1")])]}),"instanceName":"1"}),"instanceName":"1"}),"instanceName":"1"}),"instanceName":"1"}),"instanceName":"1"}),"instanceName":"1"}),"instanceName":"1"});
            var Q1459;
            Q1459=makeQuery(id+"F12.opPattern","COPY",BODY,{"derivedFrom":makeQuery(id+"F11.opPattern","COPY",BODY,{"derivedFrom":makeQuery(id+"F10.opPattern","COPY",BODY,{"derivedFrom":makeQuery(id+"F9.opPattern","COPY",BODY,{"derivedFrom":makeQuery(id+"F6.opPattern","COPY",BODY,{"derivedFrom":makeQuery(id+"F5.opPattern","COPY",BODY,{"derivedFrom":makeQuery(id+"F3.opPattern","COPY",BODY,{"derivedFrom":makeQuery(id+"F2.opPattern","COPY",BODY,{"derivedFrom":makeQuery(id+"F1.opRevolve","SWEPT_BODY",BODY,{"disambiguationData":[OSD([sQuery(id+"F0.wireOp",EDGE,"E1")])]}),"instanceName":"1"}),"instanceName":"1"}),"instanceName":"1"}),"instanceName":"1"}),"instanceName":"1"}),"instanceName":"1"}),"instanceName":"1"}),"instanceName":"1"});
            var Q1460;
            Q1460=makeQuery(id+"F12.opPattern","COPY",BODY,{"derivedFrom":makeQuery(id+"F11.opPattern","COPY",BODY,{"derivedFrom":makeQuery(id+"F10.opPattern","COPY",BODY,{"derivedFrom":makeQuery(id+"F9.opPattern","COPY",BODY,{"derivedFrom":makeQuery(id+"F6.opPattern","COPY",BODY,{"derivedFrom":makeQuery(id+"F5.opPattern","COPY",BODY,{"derivedFrom":makeQuery(id+"F4.opPattern","COPY",BODY,{"derivedFrom":makeQuery(id+"F1.opRevolve","SWEPT_BODY",BODY,{"disambiguationData":[OSD([sQuery(id+"F0.wireOp",EDGE,"E1")])]}),"instanceName":"1"}),"instanceName":"1"}),"instanceName":"1"}),"instanceName":"1"}),"instanceName":"1"}),"instanceName":"1"}),"instanceName":"1"});
            var Q1461;
            Q1461=makeQuery(id+"F12.opPattern","COPY",BODY,{"derivedFrom":makeQuery(id+"F11.opPattern","COPY",BODY,{"derivedFrom":makeQuery(id+"F10.opPattern","COPY",BODY,{"derivedFrom":makeQuery(id+"F9.opPattern","COPY",BODY,{"derivedFrom":makeQuery(id+"F6.opPattern","COPY",BODY,{"derivedFrom":makeQuery(id+"F5.opPattern","COPY",BODY,{"derivedFrom":makeQuery(id+"F4.opPattern","COPY",BODY,{"derivedFrom":makeQuery(id+"F2.opPattern","COPY",BODY,{"derivedFrom":makeQuery(id+"F1.opRevolve","SWEPT_BODY",BODY,{"disambiguationData":[OSD([sQuery(id+"F0.wireOp",EDGE,"E1")])]}),"instanceName":"1"}),"instanceName":"1"}),"instanceName":"1"}),"instanceName":"1"}),"instanceName":"1"}),"instanceName":"1"}),"instanceName":"1"}),"instanceName":"1"});
            var Q1462;
            Q1462=makeQuery(id+"F12.opPattern","COPY",BODY,{"derivedFrom":makeQuery(id+"F11.opPattern","COPY",BODY,{"derivedFrom":makeQuery(id+"F10.opPattern","COPY",BODY,{"derivedFrom":makeQuery(id+"F9.opPattern","COPY",BODY,{"derivedFrom":makeQuery(id+"F6.opPattern","COPY",BODY,{"derivedFrom":makeQuery(id+"F5.opPattern","COPY",BODY,{"derivedFrom":makeQuery(id+"F4.opPattern","COPY",BODY,{"derivedFrom":makeQuery(id+"F3.opPattern","COPY",BODY,{"derivedFrom":makeQuery(id+"F2.opPattern","COPY",BODY,{"derivedFrom":makeQuery(id+"F1.opRevolve","SWEPT_BODY",BODY,{"disambiguationData":[OSD([sQuery(id+"F0.wireOp",EDGE,"E1")])]}),"instanceName":"1"}),"instanceName":"1"}),"instanceName":"1"}),"instanceName":"1"}),"instanceName":"1"}),"instanceName":"1"}),"instanceName":"1"}),"instanceName":"1"}),"instanceName":"1"});
            var Q1463;
            Q1463=makeQuery(id+"F12.opPattern","COPY",BODY,{"derivedFrom":makeQuery(id+"F11.opPattern","COPY",BODY,{"derivedFrom":makeQuery(id+"F10.opPattern","COPY",BODY,{"derivedFrom":makeQuery(id+"F9.opPattern","COPY",BODY,{"derivedFrom":makeQuery(id+"F7.opPattern","COPY",BODY,{"derivedFrom":makeQuery(id+"F1.opRevolve","SWEPT_BODY",BODY,{"disambiguationData":[OSD([sQuery(id+"F0.wireOp",EDGE,"E1")])]}),"instanceName":"1"}),"instanceName":"1"}),"instanceName":"1"}),"instanceName":"1"}),"instanceName":"1"});
            var Q1464;
            Q1464=makeQuery(id+"F12.opPattern","COPY",BODY,{"derivedFrom":makeQuery(id+"F11.opPattern","COPY",BODY,{"derivedFrom":makeQuery(id+"F10.opPattern","COPY",BODY,{"derivedFrom":makeQuery(id+"F9.opPattern","COPY",BODY,{"derivedFrom":makeQuery(id+"F7.opPattern","COPY",BODY,{"derivedFrom":makeQuery(id+"F2.opPattern","COPY",BODY,{"derivedFrom":makeQuery(id+"F1.opRevolve","SWEPT_BODY",BODY,{"disambiguationData":[OSD([sQuery(id+"F0.wireOp",EDGE,"E1")])]}),"instanceName":"1"}),"instanceName":"1"}),"instanceName":"1"}),"instanceName":"1"}),"instanceName":"1"}),"instanceName":"1"});
            var Q1465;
            Q1465=makeQuery(id+"F12.opPattern","COPY",BODY,{"derivedFrom":makeQuery(id+"F11.opPattern","COPY",BODY,{"derivedFrom":makeQuery(id+"F10.opPattern","COPY",BODY,{"derivedFrom":makeQuery(id+"F9.opPattern","COPY",BODY,{"derivedFrom":makeQuery(id+"F7.opPattern","COPY",BODY,{"derivedFrom":makeQuery(id+"F3.opPattern","COPY",BODY,{"derivedFrom":makeQuery(id+"F2.opPattern","COPY",BODY,{"derivedFrom":makeQuery(id+"F1.opRevolve","SWEPT_BODY",BODY,{"disambiguationData":[OSD([sQuery(id+"F0.wireOp",EDGE,"E1")])]}),"instanceName":"1"}),"instanceName":"1"}),"instanceName":"1"}),"instanceName":"1"}),"instanceName":"1"}),"instanceName":"1"}),"instanceName":"1"});
            var Q1466;
            Q1466=makeQuery(id+"F12.opPattern","COPY",BODY,{"derivedFrom":makeQuery(id+"F11.opPattern","COPY",BODY,{"derivedFrom":makeQuery(id+"F10.opPattern","COPY",BODY,{"derivedFrom":makeQuery(id+"F9.opPattern","COPY",BODY,{"derivedFrom":makeQuery(id+"F7.opPattern","COPY",BODY,{"derivedFrom":makeQuery(id+"F4.opPattern","COPY",BODY,{"derivedFrom":makeQuery(id+"F1.opRevolve","SWEPT_BODY",BODY,{"disambiguationData":[OSD([sQuery(id+"F0.wireOp",EDGE,"E1")])]}),"instanceName":"1"}),"instanceName":"1"}),"instanceName":"1"}),"instanceName":"1"}),"instanceName":"1"}),"instanceName":"1"});
            var Q1467;
            Q1467=makeQuery(id+"F12.opPattern","COPY",BODY,{"derivedFrom":makeQuery(id+"F11.opPattern","COPY",BODY,{"derivedFrom":makeQuery(id+"F10.opPattern","COPY",BODY,{"derivedFrom":makeQuery(id+"F9.opPattern","COPY",BODY,{"derivedFrom":makeQuery(id+"F7.opPattern","COPY",BODY,{"derivedFrom":makeQuery(id+"F4.opPattern","COPY",BODY,{"derivedFrom":makeQuery(id+"F2.opPattern","COPY",BODY,{"derivedFrom":makeQuery(id+"F1.opRevolve","SWEPT_BODY",BODY,{"disambiguationData":[OSD([sQuery(id+"F0.wireOp",EDGE,"E1")])]}),"instanceName":"1"}),"instanceName":"1"}),"instanceName":"1"}),"instanceName":"1"}),"instanceName":"1"}),"instanceName":"1"}),"instanceName":"1"});
            var Q1468;
            Q1468=makeQuery(id+"F12.opPattern","COPY",BODY,{"derivedFrom":makeQuery(id+"F11.opPattern","COPY",BODY,{"derivedFrom":makeQuery(id+"F10.opPattern","COPY",BODY,{"derivedFrom":makeQuery(id+"F9.opPattern","COPY",BODY,{"derivedFrom":makeQuery(id+"F7.opPattern","COPY",BODY,{"derivedFrom":makeQuery(id+"F4.opPattern","COPY",BODY,{"derivedFrom":makeQuery(id+"F3.opPattern","COPY",BODY,{"derivedFrom":makeQuery(id+"F2.opPattern","COPY",BODY,{"derivedFrom":makeQuery(id+"F1.opRevolve","SWEPT_BODY",BODY,{"disambiguationData":[OSD([sQuery(id+"F0.wireOp",EDGE,"E1")])]}),"instanceName":"1"}),"instanceName":"1"}),"instanceName":"1"}),"instanceName":"1"}),"instanceName":"1"}),"instanceName":"1"}),"instanceName":"1"}),"instanceName":"1"});
            var Q1469;
            Q1469=makeQuery(id+"F12.opPattern","COPY",BODY,{"derivedFrom":makeQuery(id+"F11.opPattern","COPY",BODY,{"derivedFrom":makeQuery(id+"F10.opPattern","COPY",BODY,{"derivedFrom":makeQuery(id+"F9.opPattern","COPY",BODY,{"derivedFrom":makeQuery(id+"F7.opPattern","COPY",BODY,{"derivedFrom":makeQuery(id+"F5.opPattern","COPY",BODY,{"derivedFrom":makeQuery(id+"F1.opRevolve","SWEPT_BODY",BODY,{"disambiguationData":[OSD([sQuery(id+"F0.wireOp",EDGE,"E1")])]}),"instanceName":"1"}),"instanceName":"1"}),"instanceName":"1"}),"instanceName":"1"}),"instanceName":"1"}),"instanceName":"1"});
            var Q1470;
            Q1470=makeQuery(id+"F12.opPattern","COPY",BODY,{"derivedFrom":makeQuery(id+"F11.opPattern","COPY",BODY,{"derivedFrom":makeQuery(id+"F10.opPattern","COPY",BODY,{"derivedFrom":makeQuery(id+"F9.opPattern","COPY",BODY,{"derivedFrom":makeQuery(id+"F7.opPattern","COPY",BODY,{"derivedFrom":makeQuery(id+"F5.opPattern","COPY",BODY,{"derivedFrom":makeQuery(id+"F2.opPattern","COPY",BODY,{"derivedFrom":makeQuery(id+"F1.opRevolve","SWEPT_BODY",BODY,{"disambiguationData":[OSD([sQuery(id+"F0.wireOp",EDGE,"E1")])]}),"instanceName":"1"}),"instanceName":"1"}),"instanceName":"1"}),"instanceName":"1"}),"instanceName":"1"}),"instanceName":"1"}),"instanceName":"1"});
            var Q1471;
            Q1471=makeQuery(id+"F12.opPattern","COPY",BODY,{"derivedFrom":makeQuery(id+"F11.opPattern","COPY",BODY,{"derivedFrom":makeQuery(id+"F10.opPattern","COPY",BODY,{"derivedFrom":makeQuery(id+"F9.opPattern","COPY",BODY,{"derivedFrom":makeQuery(id+"F7.opPattern","COPY",BODY,{"derivedFrom":makeQuery(id+"F5.opPattern","COPY",BODY,{"derivedFrom":makeQuery(id+"F3.opPattern","COPY",BODY,{"derivedFrom":makeQuery(id+"F2.opPattern","COPY",BODY,{"derivedFrom":makeQuery(id+"F1.opRevolve","SWEPT_BODY",BODY,{"disambiguationData":[OSD([sQuery(id+"F0.wireOp",EDGE,"E1")])]}),"instanceName":"1"}),"instanceName":"1"}),"instanceName":"1"}),"instanceName":"1"}),"instanceName":"1"}),"instanceName":"1"}),"instanceName":"1"}),"instanceName":"1"});
            var Q1472;
            Q1472=makeQuery(id+"F12.opPattern","COPY",BODY,{"derivedFrom":makeQuery(id+"F11.opPattern","COPY",BODY,{"derivedFrom":makeQuery(id+"F10.opPattern","COPY",BODY,{"derivedFrom":makeQuery(id+"F9.opPattern","COPY",BODY,{"derivedFrom":makeQuery(id+"F7.opPattern","COPY",BODY,{"derivedFrom":makeQuery(id+"F5.opPattern","COPY",BODY,{"derivedFrom":makeQuery(id+"F4.opPattern","COPY",BODY,{"derivedFrom":makeQuery(id+"F1.opRevolve","SWEPT_BODY",BODY,{"disambiguationData":[OSD([sQuery(id+"F0.wireOp",EDGE,"E1")])]}),"instanceName":"1"}),"instanceName":"1"}),"instanceName":"1"}),"instanceName":"1"}),"instanceName":"1"}),"instanceName":"1"}),"instanceName":"1"});
            var Q1473;
            Q1473=makeQuery(id+"F12.opPattern","COPY",BODY,{"derivedFrom":makeQuery(id+"F11.opPattern","COPY",BODY,{"derivedFrom":makeQuery(id+"F10.opPattern","COPY",BODY,{"derivedFrom":makeQuery(id+"F9.opPattern","COPY",BODY,{"derivedFrom":makeQuery(id+"F7.opPattern","COPY",BODY,{"derivedFrom":makeQuery(id+"F5.opPattern","COPY",BODY,{"derivedFrom":makeQuery(id+"F4.opPattern","COPY",BODY,{"derivedFrom":makeQuery(id+"F2.opPattern","COPY",BODY,{"derivedFrom":makeQuery(id+"F1.opRevolve","SWEPT_BODY",BODY,{"disambiguationData":[OSD([sQuery(id+"F0.wireOp",EDGE,"E1")])]}),"instanceName":"1"}),"instanceName":"1"}),"instanceName":"1"}),"instanceName":"1"}),"instanceName":"1"}),"instanceName":"1"}),"instanceName":"1"}),"instanceName":"1"});
            var Q1474;
            Q1474=makeQuery(id+"F12.opPattern","COPY",BODY,{"derivedFrom":makeQuery(id+"F11.opPattern","COPY",BODY,{"derivedFrom":makeQuery(id+"F10.opPattern","COPY",BODY,{"derivedFrom":makeQuery(id+"F9.opPattern","COPY",BODY,{"derivedFrom":makeQuery(id+"F7.opPattern","COPY",BODY,{"derivedFrom":makeQuery(id+"F5.opPattern","COPY",BODY,{"derivedFrom":makeQuery(id+"F4.opPattern","COPY",BODY,{"derivedFrom":makeQuery(id+"F3.opPattern","COPY",BODY,{"derivedFrom":makeQuery(id+"F2.opPattern","COPY",BODY,{"derivedFrom":makeQuery(id+"F1.opRevolve","SWEPT_BODY",BODY,{"disambiguationData":[OSD([sQuery(id+"F0.wireOp",EDGE,"E1")])]}),"instanceName":"1"}),"instanceName":"1"}),"instanceName":"1"}),"instanceName":"1"}),"instanceName":"1"}),"instanceName":"1"}),"instanceName":"1"}),"instanceName":"1"}),"instanceName":"1"});
            var Q1475;
            Q1475=makeQuery(id+"F12.opPattern","COPY",BODY,{"derivedFrom":makeQuery(id+"F11.opPattern","COPY",BODY,{"derivedFrom":makeQuery(id+"F10.opPattern","COPY",BODY,{"derivedFrom":makeQuery(id+"F9.opPattern","COPY",BODY,{"derivedFrom":makeQuery(id+"F7.opPattern","COPY",BODY,{"derivedFrom":makeQuery(id+"F6.opPattern","COPY",BODY,{"derivedFrom":makeQuery(id+"F1.opRevolve","SWEPT_BODY",BODY,{"disambiguationData":[OSD([sQuery(id+"F0.wireOp",EDGE,"E1")])]}),"instanceName":"1"}),"instanceName":"1"}),"instanceName":"1"}),"instanceName":"1"}),"instanceName":"1"}),"instanceName":"1"});
            var Q1476;
            Q1476=makeQuery(id+"F12.opPattern","COPY",BODY,{"derivedFrom":makeQuery(id+"F11.opPattern","COPY",BODY,{"derivedFrom":makeQuery(id+"F10.opPattern","COPY",BODY,{"derivedFrom":makeQuery(id+"F9.opPattern","COPY",BODY,{"derivedFrom":makeQuery(id+"F7.opPattern","COPY",BODY,{"derivedFrom":makeQuery(id+"F6.opPattern","COPY",BODY,{"derivedFrom":makeQuery(id+"F2.opPattern","COPY",BODY,{"derivedFrom":makeQuery(id+"F1.opRevolve","SWEPT_BODY",BODY,{"disambiguationData":[OSD([sQuery(id+"F0.wireOp",EDGE,"E1")])]}),"instanceName":"1"}),"instanceName":"1"}),"instanceName":"1"}),"instanceName":"1"}),"instanceName":"1"}),"instanceName":"1"}),"instanceName":"1"});
            var Q1477;
            Q1477=makeQuery(id+"F12.opPattern","COPY",BODY,{"derivedFrom":makeQuery(id+"F11.opPattern","COPY",BODY,{"derivedFrom":makeQuery(id+"F10.opPattern","COPY",BODY,{"derivedFrom":makeQuery(id+"F9.opPattern","COPY",BODY,{"derivedFrom":makeQuery(id+"F7.opPattern","COPY",BODY,{"derivedFrom":makeQuery(id+"F6.opPattern","COPY",BODY,{"derivedFrom":makeQuery(id+"F3.opPattern","COPY",BODY,{"derivedFrom":makeQuery(id+"F2.opPattern","COPY",BODY,{"derivedFrom":makeQuery(id+"F1.opRevolve","SWEPT_BODY",BODY,{"disambiguationData":[OSD([sQuery(id+"F0.wireOp",EDGE,"E1")])]}),"instanceName":"1"}),"instanceName":"1"}),"instanceName":"1"}),"instanceName":"1"}),"instanceName":"1"}),"instanceName":"1"}),"instanceName":"1"}),"instanceName":"1"});
            var Q1478;
            Q1478=makeQuery(id+"F12.opPattern","COPY",BODY,{"derivedFrom":makeQuery(id+"F11.opPattern","COPY",BODY,{"derivedFrom":makeQuery(id+"F10.opPattern","COPY",BODY,{"derivedFrom":makeQuery(id+"F9.opPattern","COPY",BODY,{"derivedFrom":makeQuery(id+"F7.opPattern","COPY",BODY,{"derivedFrom":makeQuery(id+"F6.opPattern","COPY",BODY,{"derivedFrom":makeQuery(id+"F4.opPattern","COPY",BODY,{"derivedFrom":makeQuery(id+"F1.opRevolve","SWEPT_BODY",BODY,{"disambiguationData":[OSD([sQuery(id+"F0.wireOp",EDGE,"E1")])]}),"instanceName":"1"}),"instanceName":"1"}),"instanceName":"1"}),"instanceName":"1"}),"instanceName":"1"}),"instanceName":"1"}),"instanceName":"1"});
            var Q1479;
            Q1479=makeQuery(id+"F12.opPattern","COPY",BODY,{"derivedFrom":makeQuery(id+"F11.opPattern","COPY",BODY,{"derivedFrom":makeQuery(id+"F10.opPattern","COPY",BODY,{"derivedFrom":makeQuery(id+"F9.opPattern","COPY",BODY,{"derivedFrom":makeQuery(id+"F7.opPattern","COPY",BODY,{"derivedFrom":makeQuery(id+"F6.opPattern","COPY",BODY,{"derivedFrom":makeQuery(id+"F4.opPattern","COPY",BODY,{"derivedFrom":makeQuery(id+"F2.opPattern","COPY",BODY,{"derivedFrom":makeQuery(id+"F1.opRevolve","SWEPT_BODY",BODY,{"disambiguationData":[OSD([sQuery(id+"F0.wireOp",EDGE,"E1")])]}),"instanceName":"1"}),"instanceName":"1"}),"instanceName":"1"}),"instanceName":"1"}),"instanceName":"1"}),"instanceName":"1"}),"instanceName":"1"}),"instanceName":"1"});
            var Q1480;
            Q1480=makeQuery(id+"F12.opPattern","COPY",BODY,{"derivedFrom":makeQuery(id+"F11.opPattern","COPY",BODY,{"derivedFrom":makeQuery(id+"F10.opPattern","COPY",BODY,{"derivedFrom":makeQuery(id+"F9.opPattern","COPY",BODY,{"derivedFrom":makeQuery(id+"F7.opPattern","COPY",BODY,{"derivedFrom":makeQuery(id+"F6.opPattern","COPY",BODY,{"derivedFrom":makeQuery(id+"F4.opPattern","COPY",BODY,{"derivedFrom":makeQuery(id+"F3.opPattern","COPY",BODY,{"derivedFrom":makeQuery(id+"F2.opPattern","COPY",BODY,{"derivedFrom":makeQuery(id+"F1.opRevolve","SWEPT_BODY",BODY,{"disambiguationData":[OSD([sQuery(id+"F0.wireOp",EDGE,"E1")])]}),"instanceName":"1"}),"instanceName":"1"}),"instanceName":"1"}),"instanceName":"1"}),"instanceName":"1"}),"instanceName":"1"}),"instanceName":"1"}),"instanceName":"1"}),"instanceName":"1"});
            var Q1481;
            Q1481=makeQuery(id+"F12.opPattern","COPY",BODY,{"derivedFrom":makeQuery(id+"F11.opPattern","COPY",BODY,{"derivedFrom":makeQuery(id+"F10.opPattern","COPY",BODY,{"derivedFrom":makeQuery(id+"F9.opPattern","COPY",BODY,{"derivedFrom":makeQuery(id+"F7.opPattern","COPY",BODY,{"derivedFrom":makeQuery(id+"F6.opPattern","COPY",BODY,{"derivedFrom":makeQuery(id+"F5.opPattern","COPY",BODY,{"derivedFrom":makeQuery(id+"F1.opRevolve","SWEPT_BODY",BODY,{"disambiguationData":[OSD([sQuery(id+"F0.wireOp",EDGE,"E1")])]}),"instanceName":"1"}),"instanceName":"1"}),"instanceName":"1"}),"instanceName":"1"}),"instanceName":"1"}),"instanceName":"1"}),"instanceName":"1"});
            var Q1482;
            Q1482=makeQuery(id+"F12.opPattern","COPY",BODY,{"derivedFrom":makeQuery(id+"F11.opPattern","COPY",BODY,{"derivedFrom":makeQuery(id+"F10.opPattern","COPY",BODY,{"derivedFrom":makeQuery(id+"F9.opPattern","COPY",BODY,{"derivedFrom":makeQuery(id+"F7.opPattern","COPY",BODY,{"derivedFrom":makeQuery(id+"F6.opPattern","COPY",BODY,{"derivedFrom":makeQuery(id+"F5.opPattern","COPY",BODY,{"derivedFrom":makeQuery(id+"F2.opPattern","COPY",BODY,{"derivedFrom":makeQuery(id+"F1.opRevolve","SWEPT_BODY",BODY,{"disambiguationData":[OSD([sQuery(id+"F0.wireOp",EDGE,"E1")])]}),"instanceName":"1"}),"instanceName":"1"}),"instanceName":"1"}),"instanceName":"1"}),"instanceName":"1"}),"instanceName":"1"}),"instanceName":"1"}),"instanceName":"1"});
            var Q1483;
            Q1483=makeQuery(id+"F12.opPattern","COPY",BODY,{"derivedFrom":makeQuery(id+"F11.opPattern","COPY",BODY,{"derivedFrom":makeQuery(id+"F10.opPattern","COPY",BODY,{"derivedFrom":makeQuery(id+"F9.opPattern","COPY",BODY,{"derivedFrom":makeQuery(id+"F7.opPattern","COPY",BODY,{"derivedFrom":makeQuery(id+"F6.opPattern","COPY",BODY,{"derivedFrom":makeQuery(id+"F5.opPattern","COPY",BODY,{"derivedFrom":makeQuery(id+"F3.opPattern","COPY",BODY,{"derivedFrom":makeQuery(id+"F2.opPattern","COPY",BODY,{"derivedFrom":makeQuery(id+"F1.opRevolve","SWEPT_BODY",BODY,{"disambiguationData":[OSD([sQuery(id+"F0.wireOp",EDGE,"E1")])]}),"instanceName":"1"}),"instanceName":"1"}),"instanceName":"1"}),"instanceName":"1"}),"instanceName":"1"}),"instanceName":"1"}),"instanceName":"1"}),"instanceName":"1"}),"instanceName":"1"});
            var Q1484;
            Q1484=makeQuery(id+"F12.opPattern","COPY",BODY,{"derivedFrom":makeQuery(id+"F11.opPattern","COPY",BODY,{"derivedFrom":makeQuery(id+"F10.opPattern","COPY",BODY,{"derivedFrom":makeQuery(id+"F9.opPattern","COPY",BODY,{"derivedFrom":makeQuery(id+"F7.opPattern","COPY",BODY,{"derivedFrom":makeQuery(id+"F6.opPattern","COPY",BODY,{"derivedFrom":makeQuery(id+"F5.opPattern","COPY",BODY,{"derivedFrom":makeQuery(id+"F4.opPattern","COPY",BODY,{"derivedFrom":makeQuery(id+"F1.opRevolve","SWEPT_BODY",BODY,{"disambiguationData":[OSD([sQuery(id+"F0.wireOp",EDGE,"E1")])]}),"instanceName":"1"}),"instanceName":"1"}),"instanceName":"1"}),"instanceName":"1"}),"instanceName":"1"}),"instanceName":"1"}),"instanceName":"1"}),"instanceName":"1"});
            var Q1485;
            Q1485=makeQuery(id+"F12.opPattern","COPY",BODY,{"derivedFrom":makeQuery(id+"F11.opPattern","COPY",BODY,{"derivedFrom":makeQuery(id+"F10.opPattern","COPY",BODY,{"derivedFrom":makeQuery(id+"F9.opPattern","COPY",BODY,{"derivedFrom":makeQuery(id+"F7.opPattern","COPY",BODY,{"derivedFrom":makeQuery(id+"F6.opPattern","COPY",BODY,{"derivedFrom":makeQuery(id+"F5.opPattern","COPY",BODY,{"derivedFrom":makeQuery(id+"F4.opPattern","COPY",BODY,{"derivedFrom":makeQuery(id+"F2.opPattern","COPY",BODY,{"derivedFrom":makeQuery(id+"F1.opRevolve","SWEPT_BODY",BODY,{"disambiguationData":[OSD([sQuery(id+"F0.wireOp",EDGE,"E1")])]}),"instanceName":"1"}),"instanceName":"1"}),"instanceName":"1"}),"instanceName":"1"}),"instanceName":"1"}),"instanceName":"1"}),"instanceName":"1"}),"instanceName":"1"}),"instanceName":"1"});
            var Q1486;
            Q1486=makeQuery(id+"F12.opPattern","COPY",BODY,{"derivedFrom":makeQuery(id+"F11.opPattern","COPY",BODY,{"derivedFrom":makeQuery(id+"F10.opPattern","COPY",BODY,{"derivedFrom":makeQuery(id+"F9.opPattern","COPY",BODY,{"derivedFrom":makeQuery(id+"F7.opPattern","COPY",BODY,{"derivedFrom":makeQuery(id+"F6.opPattern","COPY",BODY,{"derivedFrom":makeQuery(id+"F5.opPattern","COPY",BODY,{"derivedFrom":makeQuery(id+"F4.opPattern","COPY",BODY,{"derivedFrom":makeQuery(id+"F3.opPattern","COPY",BODY,{"derivedFrom":makeQuery(id+"F2.opPattern","COPY",BODY,{"derivedFrom":makeQuery(id+"F1.opRevolve","SWEPT_BODY",BODY,{"disambiguationData":[OSD([sQuery(id+"F0.wireOp",EDGE,"E1")])]}),"instanceName":"1"}),"instanceName":"1"}),"instanceName":"1"}),"instanceName":"1"}),"instanceName":"1"}),"instanceName":"1"}),"instanceName":"1"}),"instanceName":"1"}),"instanceName":"1"}),"instanceName":"1"});
            var Q1487;
            Q1487=makeQuery(id+"F12.opPattern","COPY",BODY,{"derivedFrom":makeQuery(id+"F11.opPattern","COPY",BODY,{"derivedFrom":makeQuery(id+"F10.opPattern","COPY",BODY,{"derivedFrom":makeQuery(id+"F9.opPattern","COPY",BODY,{"derivedFrom":makeQuery(id+"F8.opPattern","COPY",BODY,{"derivedFrom":makeQuery(id+"F1.opRevolve","SWEPT_BODY",BODY,{"disambiguationData":[OSD([sQuery(id+"F0.wireOp",EDGE,"E1")])]}),"instanceName":"1"}),"instanceName":"1"}),"instanceName":"1"}),"instanceName":"1"}),"instanceName":"1"});
            var Q1488;
            Q1488=makeQuery(id+"F12.opPattern","COPY",BODY,{"derivedFrom":makeQuery(id+"F11.opPattern","COPY",BODY,{"derivedFrom":makeQuery(id+"F10.opPattern","COPY",BODY,{"derivedFrom":makeQuery(id+"F9.opPattern","COPY",BODY,{"derivedFrom":makeQuery(id+"F8.opPattern","COPY",BODY,{"derivedFrom":makeQuery(id+"F2.opPattern","COPY",BODY,{"derivedFrom":makeQuery(id+"F1.opRevolve","SWEPT_BODY",BODY,{"disambiguationData":[OSD([sQuery(id+"F0.wireOp",EDGE,"E1")])]}),"instanceName":"1"}),"instanceName":"1"}),"instanceName":"1"}),"instanceName":"1"}),"instanceName":"1"}),"instanceName":"1"});
            var Q1489;
            Q1489=makeQuery(id+"F12.opPattern","COPY",BODY,{"derivedFrom":makeQuery(id+"F11.opPattern","COPY",BODY,{"derivedFrom":makeQuery(id+"F10.opPattern","COPY",BODY,{"derivedFrom":makeQuery(id+"F9.opPattern","COPY",BODY,{"derivedFrom":makeQuery(id+"F8.opPattern","COPY",BODY,{"derivedFrom":makeQuery(id+"F3.opPattern","COPY",BODY,{"derivedFrom":makeQuery(id+"F2.opPattern","COPY",BODY,{"derivedFrom":makeQuery(id+"F1.opRevolve","SWEPT_BODY",BODY,{"disambiguationData":[OSD([sQuery(id+"F0.wireOp",EDGE,"E1")])]}),"instanceName":"1"}),"instanceName":"1"}),"instanceName":"1"}),"instanceName":"1"}),"instanceName":"1"}),"instanceName":"1"}),"instanceName":"1"});
            var Q1490;
            Q1490=makeQuery(id+"F12.opPattern","COPY",BODY,{"derivedFrom":makeQuery(id+"F11.opPattern","COPY",BODY,{"derivedFrom":makeQuery(id+"F10.opPattern","COPY",BODY,{"derivedFrom":makeQuery(id+"F9.opPattern","COPY",BODY,{"derivedFrom":makeQuery(id+"F8.opPattern","COPY",BODY,{"derivedFrom":makeQuery(id+"F4.opPattern","COPY",BODY,{"derivedFrom":makeQuery(id+"F1.opRevolve","SWEPT_BODY",BODY,{"disambiguationData":[OSD([sQuery(id+"F0.wireOp",EDGE,"E1")])]}),"instanceName":"1"}),"instanceName":"1"}),"instanceName":"1"}),"instanceName":"1"}),"instanceName":"1"}),"instanceName":"1"});
            var Q1491;
            Q1491=makeQuery(id+"F12.opPattern","COPY",BODY,{"derivedFrom":makeQuery(id+"F11.opPattern","COPY",BODY,{"derivedFrom":makeQuery(id+"F10.opPattern","COPY",BODY,{"derivedFrom":makeQuery(id+"F9.opPattern","COPY",BODY,{"derivedFrom":makeQuery(id+"F8.opPattern","COPY",BODY,{"derivedFrom":makeQuery(id+"F4.opPattern","COPY",BODY,{"derivedFrom":makeQuery(id+"F2.opPattern","COPY",BODY,{"derivedFrom":makeQuery(id+"F1.opRevolve","SWEPT_BODY",BODY,{"disambiguationData":[OSD([sQuery(id+"F0.wireOp",EDGE,"E1")])]}),"instanceName":"1"}),"instanceName":"1"}),"instanceName":"1"}),"instanceName":"1"}),"instanceName":"1"}),"instanceName":"1"}),"instanceName":"1"});
            var Q1492;
            Q1492=makeQuery(id+"F12.opPattern","COPY",BODY,{"derivedFrom":makeQuery(id+"F11.opPattern","COPY",BODY,{"derivedFrom":makeQuery(id+"F10.opPattern","COPY",BODY,{"derivedFrom":makeQuery(id+"F9.opPattern","COPY",BODY,{"derivedFrom":makeQuery(id+"F8.opPattern","COPY",BODY,{"derivedFrom":makeQuery(id+"F4.opPattern","COPY",BODY,{"derivedFrom":makeQuery(id+"F3.opPattern","COPY",BODY,{"derivedFrom":makeQuery(id+"F2.opPattern","COPY",BODY,{"derivedFrom":makeQuery(id+"F1.opRevolve","SWEPT_BODY",BODY,{"disambiguationData":[OSD([sQuery(id+"F0.wireOp",EDGE,"E1")])]}),"instanceName":"1"}),"instanceName":"1"}),"instanceName":"1"}),"instanceName":"1"}),"instanceName":"1"}),"instanceName":"1"}),"instanceName":"1"}),"instanceName":"1"});
            var Q1493;
            Q1493=makeQuery(id+"F12.opPattern","COPY",BODY,{"derivedFrom":makeQuery(id+"F11.opPattern","COPY",BODY,{"derivedFrom":makeQuery(id+"F10.opPattern","COPY",BODY,{"derivedFrom":makeQuery(id+"F9.opPattern","COPY",BODY,{"derivedFrom":makeQuery(id+"F8.opPattern","COPY",BODY,{"derivedFrom":makeQuery(id+"F5.opPattern","COPY",BODY,{"derivedFrom":makeQuery(id+"F1.opRevolve","SWEPT_BODY",BODY,{"disambiguationData":[OSD([sQuery(id+"F0.wireOp",EDGE,"E1")])]}),"instanceName":"1"}),"instanceName":"1"}),"instanceName":"1"}),"instanceName":"1"}),"instanceName":"1"}),"instanceName":"1"});
            var Q1494;
            Q1494=makeQuery(id+"F12.opPattern","COPY",BODY,{"derivedFrom":makeQuery(id+"F11.opPattern","COPY",BODY,{"derivedFrom":makeQuery(id+"F10.opPattern","COPY",BODY,{"derivedFrom":makeQuery(id+"F9.opPattern","COPY",BODY,{"derivedFrom":makeQuery(id+"F8.opPattern","COPY",BODY,{"derivedFrom":makeQuery(id+"F5.opPattern","COPY",BODY,{"derivedFrom":makeQuery(id+"F2.opPattern","COPY",BODY,{"derivedFrom":makeQuery(id+"F1.opRevolve","SWEPT_BODY",BODY,{"disambiguationData":[OSD([sQuery(id+"F0.wireOp",EDGE,"E1")])]}),"instanceName":"1"}),"instanceName":"1"}),"instanceName":"1"}),"instanceName":"1"}),"instanceName":"1"}),"instanceName":"1"}),"instanceName":"1"});
            var Q1495;
            Q1495=makeQuery(id+"F12.opPattern","COPY",BODY,{"derivedFrom":makeQuery(id+"F11.opPattern","COPY",BODY,{"derivedFrom":makeQuery(id+"F10.opPattern","COPY",BODY,{"derivedFrom":makeQuery(id+"F9.opPattern","COPY",BODY,{"derivedFrom":makeQuery(id+"F8.opPattern","COPY",BODY,{"derivedFrom":makeQuery(id+"F5.opPattern","COPY",BODY,{"derivedFrom":makeQuery(id+"F3.opPattern","COPY",BODY,{"derivedFrom":makeQuery(id+"F2.opPattern","COPY",BODY,{"derivedFrom":makeQuery(id+"F1.opRevolve","SWEPT_BODY",BODY,{"disambiguationData":[OSD([sQuery(id+"F0.wireOp",EDGE,"E1")])]}),"instanceName":"1"}),"instanceName":"1"}),"instanceName":"1"}),"instanceName":"1"}),"instanceName":"1"}),"instanceName":"1"}),"instanceName":"1"}),"instanceName":"1"});
            var Q1496;
            Q1496=makeQuery(id+"F12.opPattern","COPY",BODY,{"derivedFrom":makeQuery(id+"F11.opPattern","COPY",BODY,{"derivedFrom":makeQuery(id+"F10.opPattern","COPY",BODY,{"derivedFrom":makeQuery(id+"F9.opPattern","COPY",BODY,{"derivedFrom":makeQuery(id+"F8.opPattern","COPY",BODY,{"derivedFrom":makeQuery(id+"F5.opPattern","COPY",BODY,{"derivedFrom":makeQuery(id+"F4.opPattern","COPY",BODY,{"derivedFrom":makeQuery(id+"F1.opRevolve","SWEPT_BODY",BODY,{"disambiguationData":[OSD([sQuery(id+"F0.wireOp",EDGE,"E1")])]}),"instanceName":"1"}),"instanceName":"1"}),"instanceName":"1"}),"instanceName":"1"}),"instanceName":"1"}),"instanceName":"1"}),"instanceName":"1"});
            var Q1497;
            Q1497=makeQuery(id+"F12.opPattern","COPY",BODY,{"derivedFrom":makeQuery(id+"F11.opPattern","COPY",BODY,{"derivedFrom":makeQuery(id+"F10.opPattern","COPY",BODY,{"derivedFrom":makeQuery(id+"F9.opPattern","COPY",BODY,{"derivedFrom":makeQuery(id+"F8.opPattern","COPY",BODY,{"derivedFrom":makeQuery(id+"F5.opPattern","COPY",BODY,{"derivedFrom":makeQuery(id+"F4.opPattern","COPY",BODY,{"derivedFrom":makeQuery(id+"F2.opPattern","COPY",BODY,{"derivedFrom":makeQuery(id+"F1.opRevolve","SWEPT_BODY",BODY,{"disambiguationData":[OSD([sQuery(id+"F0.wireOp",EDGE,"E1")])]}),"instanceName":"1"}),"instanceName":"1"}),"instanceName":"1"}),"instanceName":"1"}),"instanceName":"1"}),"instanceName":"1"}),"instanceName":"1"}),"instanceName":"1"});
            var Q1498;
            Q1498=makeQuery(id+"F12.opPattern","COPY",BODY,{"derivedFrom":makeQuery(id+"F11.opPattern","COPY",BODY,{"derivedFrom":makeQuery(id+"F10.opPattern","COPY",BODY,{"derivedFrom":makeQuery(id+"F9.opPattern","COPY",BODY,{"derivedFrom":makeQuery(id+"F8.opPattern","COPY",BODY,{"derivedFrom":makeQuery(id+"F5.opPattern","COPY",BODY,{"derivedFrom":makeQuery(id+"F4.opPattern","COPY",BODY,{"derivedFrom":makeQuery(id+"F3.opPattern","COPY",BODY,{"derivedFrom":makeQuery(id+"F2.opPattern","COPY",BODY,{"derivedFrom":makeQuery(id+"F1.opRevolve","SWEPT_BODY",BODY,{"disambiguationData":[OSD([sQuery(id+"F0.wireOp",EDGE,"E1")])]}),"instanceName":"1"}),"instanceName":"1"}),"instanceName":"1"}),"instanceName":"1"}),"instanceName":"1"}),"instanceName":"1"}),"instanceName":"1"}),"instanceName":"1"}),"instanceName":"1"});
            var Q1499;
            Q1499=makeQuery(id+"F12.opPattern","COPY",BODY,{"derivedFrom":makeQuery(id+"F11.opPattern","COPY",BODY,{"derivedFrom":makeQuery(id+"F10.opPattern","COPY",BODY,{"derivedFrom":makeQuery(id+"F9.opPattern","COPY",BODY,{"derivedFrom":makeQuery(id+"F8.opPattern","COPY",BODY,{"derivedFrom":makeQuery(id+"F6.opPattern","COPY",BODY,{"derivedFrom":makeQuery(id+"F1.opRevolve","SWEPT_BODY",BODY,{"disambiguationData":[OSD([sQuery(id+"F0.wireOp",EDGE,"E1")])]}),"instanceName":"1"}),"instanceName":"1"}),"instanceName":"1"}),"instanceName":"1"}),"instanceName":"1"}),"instanceName":"1"});
            var Q1500;
            Q1500=makeQuery(id+"F12.opPattern","COPY",BODY,{"derivedFrom":makeQuery(id+"F11.opPattern","COPY",BODY,{"derivedFrom":makeQuery(id+"F10.opPattern","COPY",BODY,{"derivedFrom":makeQuery(id+"F9.opPattern","COPY",BODY,{"derivedFrom":makeQuery(id+"F8.opPattern","COPY",BODY,{"derivedFrom":makeQuery(id+"F6.opPattern","COPY",BODY,{"derivedFrom":makeQuery(id+"F2.opPattern","COPY",BODY,{"derivedFrom":makeQuery(id+"F1.opRevolve","SWEPT_BODY",BODY,{"disambiguationData":[OSD([sQuery(id+"F0.wireOp",EDGE,"E1")])]}),"instanceName":"1"}),"instanceName":"1"}),"instanceName":"1"}),"instanceName":"1"}),"instanceName":"1"}),"instanceName":"1"}),"instanceName":"1"});
            var Q1501;
            Q1501=makeQuery(id+"F12.opPattern","COPY",BODY,{"derivedFrom":makeQuery(id+"F11.opPattern","COPY",BODY,{"derivedFrom":makeQuery(id+"F10.opPattern","COPY",BODY,{"derivedFrom":makeQuery(id+"F9.opPattern","COPY",BODY,{"derivedFrom":makeQuery(id+"F8.opPattern","COPY",BODY,{"derivedFrom":makeQuery(id+"F6.opPattern","COPY",BODY,{"derivedFrom":makeQuery(id+"F3.opPattern","COPY",BODY,{"derivedFrom":makeQuery(id+"F2.opPattern","COPY",BODY,{"derivedFrom":makeQuery(id+"F1.opRevolve","SWEPT_BODY",BODY,{"disambiguationData":[OSD([sQuery(id+"F0.wireOp",EDGE,"E1")])]}),"instanceName":"1"}),"instanceName":"1"}),"instanceName":"1"}),"instanceName":"1"}),"instanceName":"1"}),"instanceName":"1"}),"instanceName":"1"}),"instanceName":"1"});
            var Q1502;
            Q1502=makeQuery(id+"F12.opPattern","COPY",BODY,{"derivedFrom":makeQuery(id+"F11.opPattern","COPY",BODY,{"derivedFrom":makeQuery(id+"F10.opPattern","COPY",BODY,{"derivedFrom":makeQuery(id+"F9.opPattern","COPY",BODY,{"derivedFrom":makeQuery(id+"F8.opPattern","COPY",BODY,{"derivedFrom":makeQuery(id+"F6.opPattern","COPY",BODY,{"derivedFrom":makeQuery(id+"F4.opPattern","COPY",BODY,{"derivedFrom":makeQuery(id+"F1.opRevolve","SWEPT_BODY",BODY,{"disambiguationData":[OSD([sQuery(id+"F0.wireOp",EDGE,"E1")])]}),"instanceName":"1"}),"instanceName":"1"}),"instanceName":"1"}),"instanceName":"1"}),"instanceName":"1"}),"instanceName":"1"}),"instanceName":"1"});
            var Q1503;
            Q1503=makeQuery(id+"F12.opPattern","COPY",BODY,{"derivedFrom":makeQuery(id+"F11.opPattern","COPY",BODY,{"derivedFrom":makeQuery(id+"F10.opPattern","COPY",BODY,{"derivedFrom":makeQuery(id+"F9.opPattern","COPY",BODY,{"derivedFrom":makeQuery(id+"F8.opPattern","COPY",BODY,{"derivedFrom":makeQuery(id+"F6.opPattern","COPY",BODY,{"derivedFrom":makeQuery(id+"F4.opPattern","COPY",BODY,{"derivedFrom":makeQuery(id+"F2.opPattern","COPY",BODY,{"derivedFrom":makeQuery(id+"F1.opRevolve","SWEPT_BODY",BODY,{"disambiguationData":[OSD([sQuery(id+"F0.wireOp",EDGE,"E1")])]}),"instanceName":"1"}),"instanceName":"1"}),"instanceName":"1"}),"instanceName":"1"}),"instanceName":"1"}),"instanceName":"1"}),"instanceName":"1"}),"instanceName":"1"});
            var Q1504;
            Q1504=makeQuery(id+"F12.opPattern","COPY",BODY,{"derivedFrom":makeQuery(id+"F11.opPattern","COPY",BODY,{"derivedFrom":makeQuery(id+"F10.opPattern","COPY",BODY,{"derivedFrom":makeQuery(id+"F9.opPattern","COPY",BODY,{"derivedFrom":makeQuery(id+"F8.opPattern","COPY",BODY,{"derivedFrom":makeQuery(id+"F6.opPattern","COPY",BODY,{"derivedFrom":makeQuery(id+"F4.opPattern","COPY",BODY,{"derivedFrom":makeQuery(id+"F3.opPattern","COPY",BODY,{"derivedFrom":makeQuery(id+"F2.opPattern","COPY",BODY,{"derivedFrom":makeQuery(id+"F1.opRevolve","SWEPT_BODY",BODY,{"disambiguationData":[OSD([sQuery(id+"F0.wireOp",EDGE,"E1")])]}),"instanceName":"1"}),"instanceName":"1"}),"instanceName":"1"}),"instanceName":"1"}),"instanceName":"1"}),"instanceName":"1"}),"instanceName":"1"}),"instanceName":"1"}),"instanceName":"1"});
            var Q1505;
            Q1505=makeQuery(id+"F12.opPattern","COPY",BODY,{"derivedFrom":makeQuery(id+"F11.opPattern","COPY",BODY,{"derivedFrom":makeQuery(id+"F10.opPattern","COPY",BODY,{"derivedFrom":makeQuery(id+"F9.opPattern","COPY",BODY,{"derivedFrom":makeQuery(id+"F8.opPattern","COPY",BODY,{"derivedFrom":makeQuery(id+"F6.opPattern","COPY",BODY,{"derivedFrom":makeQuery(id+"F5.opPattern","COPY",BODY,{"derivedFrom":makeQuery(id+"F1.opRevolve","SWEPT_BODY",BODY,{"disambiguationData":[OSD([sQuery(id+"F0.wireOp",EDGE,"E1")])]}),"instanceName":"1"}),"instanceName":"1"}),"instanceName":"1"}),"instanceName":"1"}),"instanceName":"1"}),"instanceName":"1"}),"instanceName":"1"});
            var Q1506;
            Q1506=makeQuery(id+"F12.opPattern","COPY",BODY,{"derivedFrom":makeQuery(id+"F11.opPattern","COPY",BODY,{"derivedFrom":makeQuery(id+"F10.opPattern","COPY",BODY,{"derivedFrom":makeQuery(id+"F9.opPattern","COPY",BODY,{"derivedFrom":makeQuery(id+"F8.opPattern","COPY",BODY,{"derivedFrom":makeQuery(id+"F6.opPattern","COPY",BODY,{"derivedFrom":makeQuery(id+"F5.opPattern","COPY",BODY,{"derivedFrom":makeQuery(id+"F2.opPattern","COPY",BODY,{"derivedFrom":makeQuery(id+"F1.opRevolve","SWEPT_BODY",BODY,{"disambiguationData":[OSD([sQuery(id+"F0.wireOp",EDGE,"E1")])]}),"instanceName":"1"}),"instanceName":"1"}),"instanceName":"1"}),"instanceName":"1"}),"instanceName":"1"}),"instanceName":"1"}),"instanceName":"1"}),"instanceName":"1"});
            var Q1507;
            Q1507=makeQuery(id+"F12.opPattern","COPY",BODY,{"derivedFrom":makeQuery(id+"F11.opPattern","COPY",BODY,{"derivedFrom":makeQuery(id+"F10.opPattern","COPY",BODY,{"derivedFrom":makeQuery(id+"F9.opPattern","COPY",BODY,{"derivedFrom":makeQuery(id+"F8.opPattern","COPY",BODY,{"derivedFrom":makeQuery(id+"F6.opPattern","COPY",BODY,{"derivedFrom":makeQuery(id+"F5.opPattern","COPY",BODY,{"derivedFrom":makeQuery(id+"F3.opPattern","COPY",BODY,{"derivedFrom":makeQuery(id+"F2.opPattern","COPY",BODY,{"derivedFrom":makeQuery(id+"F1.opRevolve","SWEPT_BODY",BODY,{"disambiguationData":[OSD([sQuery(id+"F0.wireOp",EDGE,"E1")])]}),"instanceName":"1"}),"instanceName":"1"}),"instanceName":"1"}),"instanceName":"1"}),"instanceName":"1"}),"instanceName":"1"}),"instanceName":"1"}),"instanceName":"1"}),"instanceName":"1"});
            var Q1508;
            Q1508=makeQuery(id+"F12.opPattern","COPY",BODY,{"derivedFrom":makeQuery(id+"F11.opPattern","COPY",BODY,{"derivedFrom":makeQuery(id+"F10.opPattern","COPY",BODY,{"derivedFrom":makeQuery(id+"F9.opPattern","COPY",BODY,{"derivedFrom":makeQuery(id+"F8.opPattern","COPY",BODY,{"derivedFrom":makeQuery(id+"F6.opPattern","COPY",BODY,{"derivedFrom":makeQuery(id+"F5.opPattern","COPY",BODY,{"derivedFrom":makeQuery(id+"F4.opPattern","COPY",BODY,{"derivedFrom":makeQuery(id+"F1.opRevolve","SWEPT_BODY",BODY,{"disambiguationData":[OSD([sQuery(id+"F0.wireOp",EDGE,"E1")])]}),"instanceName":"1"}),"instanceName":"1"}),"instanceName":"1"}),"instanceName":"1"}),"instanceName":"1"}),"instanceName":"1"}),"instanceName":"1"}),"instanceName":"1"});
            var Q1509;
            Q1509=makeQuery(id+"F12.opPattern","COPY",BODY,{"derivedFrom":makeQuery(id+"F11.opPattern","COPY",BODY,{"derivedFrom":makeQuery(id+"F10.opPattern","COPY",BODY,{"derivedFrom":makeQuery(id+"F9.opPattern","COPY",BODY,{"derivedFrom":makeQuery(id+"F8.opPattern","COPY",BODY,{"derivedFrom":makeQuery(id+"F6.opPattern","COPY",BODY,{"derivedFrom":makeQuery(id+"F5.opPattern","COPY",BODY,{"derivedFrom":makeQuery(id+"F4.opPattern","COPY",BODY,{"derivedFrom":makeQuery(id+"F2.opPattern","COPY",BODY,{"derivedFrom":makeQuery(id+"F1.opRevolve","SWEPT_BODY",BODY,{"disambiguationData":[OSD([sQuery(id+"F0.wireOp",EDGE,"E1")])]}),"instanceName":"1"}),"instanceName":"1"}),"instanceName":"1"}),"instanceName":"1"}),"instanceName":"1"}),"instanceName":"1"}),"instanceName":"1"}),"instanceName":"1"}),"instanceName":"1"});
            var Q1510;
            Q1510=makeQuery(id+"F12.opPattern","COPY",BODY,{"derivedFrom":makeQuery(id+"F11.opPattern","COPY",BODY,{"derivedFrom":makeQuery(id+"F10.opPattern","COPY",BODY,{"derivedFrom":makeQuery(id+"F9.opPattern","COPY",BODY,{"derivedFrom":makeQuery(id+"F8.opPattern","COPY",BODY,{"derivedFrom":makeQuery(id+"F6.opPattern","COPY",BODY,{"derivedFrom":makeQuery(id+"F5.opPattern","COPY",BODY,{"derivedFrom":makeQuery(id+"F4.opPattern","COPY",BODY,{"derivedFrom":makeQuery(id+"F3.opPattern","COPY",BODY,{"derivedFrom":makeQuery(id+"F2.opPattern","COPY",BODY,{"derivedFrom":makeQuery(id+"F1.opRevolve","SWEPT_BODY",BODY,{"disambiguationData":[OSD([sQuery(id+"F0.wireOp",EDGE,"E1")])]}),"instanceName":"1"}),"instanceName":"1"}),"instanceName":"1"}),"instanceName":"1"}),"instanceName":"1"}),"instanceName":"1"}),"instanceName":"1"}),"instanceName":"1"}),"instanceName":"1"}),"instanceName":"1"});
            var Q1511;
            Q1511=makeQuery(id+"F12.opPattern","COPY",BODY,{"derivedFrom":makeQuery(id+"F11.opPattern","COPY",BODY,{"derivedFrom":makeQuery(id+"F10.opPattern","COPY",BODY,{"derivedFrom":makeQuery(id+"F9.opPattern","COPY",BODY,{"derivedFrom":makeQuery(id+"F8.opPattern","COPY",BODY,{"derivedFrom":makeQuery(id+"F7.opPattern","COPY",BODY,{"derivedFrom":makeQuery(id+"F1.opRevolve","SWEPT_BODY",BODY,{"disambiguationData":[OSD([sQuery(id+"F0.wireOp",EDGE,"E1")])]}),"instanceName":"1"}),"instanceName":"1"}),"instanceName":"1"}),"instanceName":"1"}),"instanceName":"1"}),"instanceName":"1"});
            var Q1512;
            Q1512=makeQuery(id+"F12.opPattern","COPY",BODY,{"derivedFrom":makeQuery(id+"F11.opPattern","COPY",BODY,{"derivedFrom":makeQuery(id+"F10.opPattern","COPY",BODY,{"derivedFrom":makeQuery(id+"F9.opPattern","COPY",BODY,{"derivedFrom":makeQuery(id+"F8.opPattern","COPY",BODY,{"derivedFrom":makeQuery(id+"F7.opPattern","COPY",BODY,{"derivedFrom":makeQuery(id+"F2.opPattern","COPY",BODY,{"derivedFrom":makeQuery(id+"F1.opRevolve","SWEPT_BODY",BODY,{"disambiguationData":[OSD([sQuery(id+"F0.wireOp",EDGE,"E1")])]}),"instanceName":"1"}),"instanceName":"1"}),"instanceName":"1"}),"instanceName":"1"}),"instanceName":"1"}),"instanceName":"1"}),"instanceName":"1"});
            var Q1513;
            Q1513=makeQuery(id+"F12.opPattern","COPY",BODY,{"derivedFrom":makeQuery(id+"F11.opPattern","COPY",BODY,{"derivedFrom":makeQuery(id+"F10.opPattern","COPY",BODY,{"derivedFrom":makeQuery(id+"F9.opPattern","COPY",BODY,{"derivedFrom":makeQuery(id+"F8.opPattern","COPY",BODY,{"derivedFrom":makeQuery(id+"F7.opPattern","COPY",BODY,{"derivedFrom":makeQuery(id+"F3.opPattern","COPY",BODY,{"derivedFrom":makeQuery(id+"F2.opPattern","COPY",BODY,{"derivedFrom":makeQuery(id+"F1.opRevolve","SWEPT_BODY",BODY,{"disambiguationData":[OSD([sQuery(id+"F0.wireOp",EDGE,"E1")])]}),"instanceName":"1"}),"instanceName":"1"}),"instanceName":"1"}),"instanceName":"1"}),"instanceName":"1"}),"instanceName":"1"}),"instanceName":"1"}),"instanceName":"1"});
            var Q1514;
            Q1514=makeQuery(id+"F12.opPattern","COPY",BODY,{"derivedFrom":makeQuery(id+"F11.opPattern","COPY",BODY,{"derivedFrom":makeQuery(id+"F10.opPattern","COPY",BODY,{"derivedFrom":makeQuery(id+"F9.opPattern","COPY",BODY,{"derivedFrom":makeQuery(id+"F8.opPattern","COPY",BODY,{"derivedFrom":makeQuery(id+"F7.opPattern","COPY",BODY,{"derivedFrom":makeQuery(id+"F4.opPattern","COPY",BODY,{"derivedFrom":makeQuery(id+"F1.opRevolve","SWEPT_BODY",BODY,{"disambiguationData":[OSD([sQuery(id+"F0.wireOp",EDGE,"E1")])]}),"instanceName":"1"}),"instanceName":"1"}),"instanceName":"1"}),"instanceName":"1"}),"instanceName":"1"}),"instanceName":"1"}),"instanceName":"1"});
            var Q1515;
            Q1515=makeQuery(id+"F12.opPattern","COPY",BODY,{"derivedFrom":makeQuery(id+"F11.opPattern","COPY",BODY,{"derivedFrom":makeQuery(id+"F10.opPattern","COPY",BODY,{"derivedFrom":makeQuery(id+"F9.opPattern","COPY",BODY,{"derivedFrom":makeQuery(id+"F8.opPattern","COPY",BODY,{"derivedFrom":makeQuery(id+"F7.opPattern","COPY",BODY,{"derivedFrom":makeQuery(id+"F4.opPattern","COPY",BODY,{"derivedFrom":makeQuery(id+"F2.opPattern","COPY",BODY,{"derivedFrom":makeQuery(id+"F1.opRevolve","SWEPT_BODY",BODY,{"disambiguationData":[OSD([sQuery(id+"F0.wireOp",EDGE,"E1")])]}),"instanceName":"1"}),"instanceName":"1"}),"instanceName":"1"}),"instanceName":"1"}),"instanceName":"1"}),"instanceName":"1"}),"instanceName":"1"}),"instanceName":"1"});
            var Q1516;
            Q1516=makeQuery(id+"F12.opPattern","COPY",BODY,{"derivedFrom":makeQuery(id+"F11.opPattern","COPY",BODY,{"derivedFrom":makeQuery(id+"F10.opPattern","COPY",BODY,{"derivedFrom":makeQuery(id+"F9.opPattern","COPY",BODY,{"derivedFrom":makeQuery(id+"F8.opPattern","COPY",BODY,{"derivedFrom":makeQuery(id+"F7.opPattern","COPY",BODY,{"derivedFrom":makeQuery(id+"F4.opPattern","COPY",BODY,{"derivedFrom":makeQuery(id+"F3.opPattern","COPY",BODY,{"derivedFrom":makeQuery(id+"F2.opPattern","COPY",BODY,{"derivedFrom":makeQuery(id+"F1.opRevolve","SWEPT_BODY",BODY,{"disambiguationData":[OSD([sQuery(id+"F0.wireOp",EDGE,"E1")])]}),"instanceName":"1"}),"instanceName":"1"}),"instanceName":"1"}),"instanceName":"1"}),"instanceName":"1"}),"instanceName":"1"}),"instanceName":"1"}),"instanceName":"1"}),"instanceName":"1"});
            var Q1517;
            Q1517=makeQuery(id+"F12.opPattern","COPY",BODY,{"derivedFrom":makeQuery(id+"F11.opPattern","COPY",BODY,{"derivedFrom":makeQuery(id+"F10.opPattern","COPY",BODY,{"derivedFrom":makeQuery(id+"F9.opPattern","COPY",BODY,{"derivedFrom":makeQuery(id+"F8.opPattern","COPY",BODY,{"derivedFrom":makeQuery(id+"F7.opPattern","COPY",BODY,{"derivedFrom":makeQuery(id+"F5.opPattern","COPY",BODY,{"derivedFrom":makeQuery(id+"F1.opRevolve","SWEPT_BODY",BODY,{"disambiguationData":[OSD([sQuery(id+"F0.wireOp",EDGE,"E1")])]}),"instanceName":"1"}),"instanceName":"1"}),"instanceName":"1"}),"instanceName":"1"}),"instanceName":"1"}),"instanceName":"1"}),"instanceName":"1"});
            var Q1518;
            Q1518=makeQuery(id+"F12.opPattern","COPY",BODY,{"derivedFrom":makeQuery(id+"F11.opPattern","COPY",BODY,{"derivedFrom":makeQuery(id+"F10.opPattern","COPY",BODY,{"derivedFrom":makeQuery(id+"F9.opPattern","COPY",BODY,{"derivedFrom":makeQuery(id+"F8.opPattern","COPY",BODY,{"derivedFrom":makeQuery(id+"F7.opPattern","COPY",BODY,{"derivedFrom":makeQuery(id+"F5.opPattern","COPY",BODY,{"derivedFrom":makeQuery(id+"F2.opPattern","COPY",BODY,{"derivedFrom":makeQuery(id+"F1.opRevolve","SWEPT_BODY",BODY,{"disambiguationData":[OSD([sQuery(id+"F0.wireOp",EDGE,"E1")])]}),"instanceName":"1"}),"instanceName":"1"}),"instanceName":"1"}),"instanceName":"1"}),"instanceName":"1"}),"instanceName":"1"}),"instanceName":"1"}),"instanceName":"1"});
            var Q1519;
            Q1519=makeQuery(id+"F12.opPattern","COPY",BODY,{"derivedFrom":makeQuery(id+"F11.opPattern","COPY",BODY,{"derivedFrom":makeQuery(id+"F10.opPattern","COPY",BODY,{"derivedFrom":makeQuery(id+"F9.opPattern","COPY",BODY,{"derivedFrom":makeQuery(id+"F8.opPattern","COPY",BODY,{"derivedFrom":makeQuery(id+"F7.opPattern","COPY",BODY,{"derivedFrom":makeQuery(id+"F5.opPattern","COPY",BODY,{"derivedFrom":makeQuery(id+"F3.opPattern","COPY",BODY,{"derivedFrom":makeQuery(id+"F2.opPattern","COPY",BODY,{"derivedFrom":makeQuery(id+"F1.opRevolve","SWEPT_BODY",BODY,{"disambiguationData":[OSD([sQuery(id+"F0.wireOp",EDGE,"E1")])]}),"instanceName":"1"}),"instanceName":"1"}),"instanceName":"1"}),"instanceName":"1"}),"instanceName":"1"}),"instanceName":"1"}),"instanceName":"1"}),"instanceName":"1"}),"instanceName":"1"});
            var Q1520;
            Q1520=makeQuery(id+"F12.opPattern","COPY",BODY,{"derivedFrom":makeQuery(id+"F11.opPattern","COPY",BODY,{"derivedFrom":makeQuery(id+"F10.opPattern","COPY",BODY,{"derivedFrom":makeQuery(id+"F9.opPattern","COPY",BODY,{"derivedFrom":makeQuery(id+"F8.opPattern","COPY",BODY,{"derivedFrom":makeQuery(id+"F7.opPattern","COPY",BODY,{"derivedFrom":makeQuery(id+"F5.opPattern","COPY",BODY,{"derivedFrom":makeQuery(id+"F4.opPattern","COPY",BODY,{"derivedFrom":makeQuery(id+"F1.opRevolve","SWEPT_BODY",BODY,{"disambiguationData":[OSD([sQuery(id+"F0.wireOp",EDGE,"E1")])]}),"instanceName":"1"}),"instanceName":"1"}),"instanceName":"1"}),"instanceName":"1"}),"instanceName":"1"}),"instanceName":"1"}),"instanceName":"1"}),"instanceName":"1"});
            var Q1521;
            Q1521=makeQuery(id+"F12.opPattern","COPY",BODY,{"derivedFrom":makeQuery(id+"F11.opPattern","COPY",BODY,{"derivedFrom":makeQuery(id+"F10.opPattern","COPY",BODY,{"derivedFrom":makeQuery(id+"F9.opPattern","COPY",BODY,{"derivedFrom":makeQuery(id+"F8.opPattern","COPY",BODY,{"derivedFrom":makeQuery(id+"F7.opPattern","COPY",BODY,{"derivedFrom":makeQuery(id+"F5.opPattern","COPY",BODY,{"derivedFrom":makeQuery(id+"F4.opPattern","COPY",BODY,{"derivedFrom":makeQuery(id+"F2.opPattern","COPY",BODY,{"derivedFrom":makeQuery(id+"F1.opRevolve","SWEPT_BODY",BODY,{"disambiguationData":[OSD([sQuery(id+"F0.wireOp",EDGE,"E1")])]}),"instanceName":"1"}),"instanceName":"1"}),"instanceName":"1"}),"instanceName":"1"}),"instanceName":"1"}),"instanceName":"1"}),"instanceName":"1"}),"instanceName":"1"}),"instanceName":"1"});
            var Q1522;
            Q1522=makeQuery(id+"F12.opPattern","COPY",BODY,{"derivedFrom":makeQuery(id+"F11.opPattern","COPY",BODY,{"derivedFrom":makeQuery(id+"F10.opPattern","COPY",BODY,{"derivedFrom":makeQuery(id+"F9.opPattern","COPY",BODY,{"derivedFrom":makeQuery(id+"F8.opPattern","COPY",BODY,{"derivedFrom":makeQuery(id+"F7.opPattern","COPY",BODY,{"derivedFrom":makeQuery(id+"F5.opPattern","COPY",BODY,{"derivedFrom":makeQuery(id+"F4.opPattern","COPY",BODY,{"derivedFrom":makeQuery(id+"F3.opPattern","COPY",BODY,{"derivedFrom":makeQuery(id+"F2.opPattern","COPY",BODY,{"derivedFrom":makeQuery(id+"F1.opRevolve","SWEPT_BODY",BODY,{"disambiguationData":[OSD([sQuery(id+"F0.wireOp",EDGE,"E1")])]}),"instanceName":"1"}),"instanceName":"1"}),"instanceName":"1"}),"instanceName":"1"}),"instanceName":"1"}),"instanceName":"1"}),"instanceName":"1"}),"instanceName":"1"}),"instanceName":"1"}),"instanceName":"1"});
            var Q1523;
            Q1523=makeQuery(id+"F12.opPattern","COPY",BODY,{"derivedFrom":makeQuery(id+"F11.opPattern","COPY",BODY,{"derivedFrom":makeQuery(id+"F10.opPattern","COPY",BODY,{"derivedFrom":makeQuery(id+"F9.opPattern","COPY",BODY,{"derivedFrom":makeQuery(id+"F8.opPattern","COPY",BODY,{"derivedFrom":makeQuery(id+"F7.opPattern","COPY",BODY,{"derivedFrom":makeQuery(id+"F6.opPattern","COPY",BODY,{"derivedFrom":makeQuery(id+"F1.opRevolve","SWEPT_BODY",BODY,{"disambiguationData":[OSD([sQuery(id+"F0.wireOp",EDGE,"E1")])]}),"instanceName":"1"}),"instanceName":"1"}),"instanceName":"1"}),"instanceName":"1"}),"instanceName":"1"}),"instanceName":"1"}),"instanceName":"1"});
            var Q1524;
            Q1524=makeQuery(id+"F12.opPattern","COPY",BODY,{"derivedFrom":makeQuery(id+"F11.opPattern","COPY",BODY,{"derivedFrom":makeQuery(id+"F10.opPattern","COPY",BODY,{"derivedFrom":makeQuery(id+"F9.opPattern","COPY",BODY,{"derivedFrom":makeQuery(id+"F8.opPattern","COPY",BODY,{"derivedFrom":makeQuery(id+"F7.opPattern","COPY",BODY,{"derivedFrom":makeQuery(id+"F6.opPattern","COPY",BODY,{"derivedFrom":makeQuery(id+"F2.opPattern","COPY",BODY,{"derivedFrom":makeQuery(id+"F1.opRevolve","SWEPT_BODY",BODY,{"disambiguationData":[OSD([sQuery(id+"F0.wireOp",EDGE,"E1")])]}),"instanceName":"1"}),"instanceName":"1"}),"instanceName":"1"}),"instanceName":"1"}),"instanceName":"1"}),"instanceName":"1"}),"instanceName":"1"}),"instanceName":"1"});
            var Q1525;
            Q1525=makeQuery(id+"F12.opPattern","COPY",BODY,{"derivedFrom":makeQuery(id+"F11.opPattern","COPY",BODY,{"derivedFrom":makeQuery(id+"F10.opPattern","COPY",BODY,{"derivedFrom":makeQuery(id+"F9.opPattern","COPY",BODY,{"derivedFrom":makeQuery(id+"F8.opPattern","COPY",BODY,{"derivedFrom":makeQuery(id+"F7.opPattern","COPY",BODY,{"derivedFrom":makeQuery(id+"F6.opPattern","COPY",BODY,{"derivedFrom":makeQuery(id+"F3.opPattern","COPY",BODY,{"derivedFrom":makeQuery(id+"F2.opPattern","COPY",BODY,{"derivedFrom":makeQuery(id+"F1.opRevolve","SWEPT_BODY",BODY,{"disambiguationData":[OSD([sQuery(id+"F0.wireOp",EDGE,"E1")])]}),"instanceName":"1"}),"instanceName":"1"}),"instanceName":"1"}),"instanceName":"1"}),"instanceName":"1"}),"instanceName":"1"}),"instanceName":"1"}),"instanceName":"1"}),"instanceName":"1"});
            var Q1526;
            Q1526=makeQuery(id+"F12.opPattern","COPY",BODY,{"derivedFrom":makeQuery(id+"F11.opPattern","COPY",BODY,{"derivedFrom":makeQuery(id+"F10.opPattern","COPY",BODY,{"derivedFrom":makeQuery(id+"F9.opPattern","COPY",BODY,{"derivedFrom":makeQuery(id+"F8.opPattern","COPY",BODY,{"derivedFrom":makeQuery(id+"F7.opPattern","COPY",BODY,{"derivedFrom":makeQuery(id+"F6.opPattern","COPY",BODY,{"derivedFrom":makeQuery(id+"F4.opPattern","COPY",BODY,{"derivedFrom":makeQuery(id+"F1.opRevolve","SWEPT_BODY",BODY,{"disambiguationData":[OSD([sQuery(id+"F0.wireOp",EDGE,"E1")])]}),"instanceName":"1"}),"instanceName":"1"}),"instanceName":"1"}),"instanceName":"1"}),"instanceName":"1"}),"instanceName":"1"}),"instanceName":"1"}),"instanceName":"1"});
            var Q1527;
            Q1527=makeQuery(id+"F12.opPattern","COPY",BODY,{"derivedFrom":makeQuery(id+"F11.opPattern","COPY",BODY,{"derivedFrom":makeQuery(id+"F10.opPattern","COPY",BODY,{"derivedFrom":makeQuery(id+"F9.opPattern","COPY",BODY,{"derivedFrom":makeQuery(id+"F8.opPattern","COPY",BODY,{"derivedFrom":makeQuery(id+"F7.opPattern","COPY",BODY,{"derivedFrom":makeQuery(id+"F6.opPattern","COPY",BODY,{"derivedFrom":makeQuery(id+"F4.opPattern","COPY",BODY,{"derivedFrom":makeQuery(id+"F2.opPattern","COPY",BODY,{"derivedFrom":makeQuery(id+"F1.opRevolve","SWEPT_BODY",BODY,{"disambiguationData":[OSD([sQuery(id+"F0.wireOp",EDGE,"E1")])]}),"instanceName":"1"}),"instanceName":"1"}),"instanceName":"1"}),"instanceName":"1"}),"instanceName":"1"}),"instanceName":"1"}),"instanceName":"1"}),"instanceName":"1"}),"instanceName":"1"});
            var Q1528;
            Q1528=makeQuery(id+"F12.opPattern","COPY",BODY,{"derivedFrom":makeQuery(id+"F11.opPattern","COPY",BODY,{"derivedFrom":makeQuery(id+"F10.opPattern","COPY",BODY,{"derivedFrom":makeQuery(id+"F9.opPattern","COPY",BODY,{"derivedFrom":makeQuery(id+"F8.opPattern","COPY",BODY,{"derivedFrom":makeQuery(id+"F7.opPattern","COPY",BODY,{"derivedFrom":makeQuery(id+"F6.opPattern","COPY",BODY,{"derivedFrom":makeQuery(id+"F4.opPattern","COPY",BODY,{"derivedFrom":makeQuery(id+"F3.opPattern","COPY",BODY,{"derivedFrom":makeQuery(id+"F2.opPattern","COPY",BODY,{"derivedFrom":makeQuery(id+"F1.opRevolve","SWEPT_BODY",BODY,{"disambiguationData":[OSD([sQuery(id+"F0.wireOp",EDGE,"E1")])]}),"instanceName":"1"}),"instanceName":"1"}),"instanceName":"1"}),"instanceName":"1"}),"instanceName":"1"}),"instanceName":"1"}),"instanceName":"1"}),"instanceName":"1"}),"instanceName":"1"}),"instanceName":"1"});
            var Q1529;
            Q1529=makeQuery(id+"F12.opPattern","COPY",BODY,{"derivedFrom":makeQuery(id+"F11.opPattern","COPY",BODY,{"derivedFrom":makeQuery(id+"F10.opPattern","COPY",BODY,{"derivedFrom":makeQuery(id+"F9.opPattern","COPY",BODY,{"derivedFrom":makeQuery(id+"F8.opPattern","COPY",BODY,{"derivedFrom":makeQuery(id+"F7.opPattern","COPY",BODY,{"derivedFrom":makeQuery(id+"F6.opPattern","COPY",BODY,{"derivedFrom":makeQuery(id+"F5.opPattern","COPY",BODY,{"derivedFrom":makeQuery(id+"F1.opRevolve","SWEPT_BODY",BODY,{"disambiguationData":[OSD([sQuery(id+"F0.wireOp",EDGE,"E1")])]}),"instanceName":"1"}),"instanceName":"1"}),"instanceName":"1"}),"instanceName":"1"}),"instanceName":"1"}),"instanceName":"1"}),"instanceName":"1"}),"instanceName":"1"});
            var Q1530;
            Q1530=makeQuery(id+"F12.opPattern","COPY",BODY,{"derivedFrom":makeQuery(id+"F11.opPattern","COPY",BODY,{"derivedFrom":makeQuery(id+"F10.opPattern","COPY",BODY,{"derivedFrom":makeQuery(id+"F9.opPattern","COPY",BODY,{"derivedFrom":makeQuery(id+"F8.opPattern","COPY",BODY,{"derivedFrom":makeQuery(id+"F7.opPattern","COPY",BODY,{"derivedFrom":makeQuery(id+"F6.opPattern","COPY",BODY,{"derivedFrom":makeQuery(id+"F5.opPattern","COPY",BODY,{"derivedFrom":makeQuery(id+"F2.opPattern","COPY",BODY,{"derivedFrom":makeQuery(id+"F1.opRevolve","SWEPT_BODY",BODY,{"disambiguationData":[OSD([sQuery(id+"F0.wireOp",EDGE,"E1")])]}),"instanceName":"1"}),"instanceName":"1"}),"instanceName":"1"}),"instanceName":"1"}),"instanceName":"1"}),"instanceName":"1"}),"instanceName":"1"}),"instanceName":"1"}),"instanceName":"1"});
            var Q1531;
            Q1531=makeQuery(id+"F12.opPattern","COPY",BODY,{"derivedFrom":makeQuery(id+"F11.opPattern","COPY",BODY,{"derivedFrom":makeQuery(id+"F10.opPattern","COPY",BODY,{"derivedFrom":makeQuery(id+"F9.opPattern","COPY",BODY,{"derivedFrom":makeQuery(id+"F8.opPattern","COPY",BODY,{"derivedFrom":makeQuery(id+"F7.opPattern","COPY",BODY,{"derivedFrom":makeQuery(id+"F6.opPattern","COPY",BODY,{"derivedFrom":makeQuery(id+"F5.opPattern","COPY",BODY,{"derivedFrom":makeQuery(id+"F3.opPattern","COPY",BODY,{"derivedFrom":makeQuery(id+"F2.opPattern","COPY",BODY,{"derivedFrom":makeQuery(id+"F1.opRevolve","SWEPT_BODY",BODY,{"disambiguationData":[OSD([sQuery(id+"F0.wireOp",EDGE,"E1")])]}),"instanceName":"1"}),"instanceName":"1"}),"instanceName":"1"}),"instanceName":"1"}),"instanceName":"1"}),"instanceName":"1"}),"instanceName":"1"}),"instanceName":"1"}),"instanceName":"1"}),"instanceName":"1"});
            var Q1532;
            Q1532=makeQuery(id+"F12.opPattern","COPY",BODY,{"derivedFrom":makeQuery(id+"F11.opPattern","COPY",BODY,{"derivedFrom":makeQuery(id+"F10.opPattern","COPY",BODY,{"derivedFrom":makeQuery(id+"F9.opPattern","COPY",BODY,{"derivedFrom":makeQuery(id+"F8.opPattern","COPY",BODY,{"derivedFrom":makeQuery(id+"F7.opPattern","COPY",BODY,{"derivedFrom":makeQuery(id+"F6.opPattern","COPY",BODY,{"derivedFrom":makeQuery(id+"F5.opPattern","COPY",BODY,{"derivedFrom":makeQuery(id+"F4.opPattern","COPY",BODY,{"derivedFrom":makeQuery(id+"F1.opRevolve","SWEPT_BODY",BODY,{"disambiguationData":[OSD([sQuery(id+"F0.wireOp",EDGE,"E1")])]}),"instanceName":"1"}),"instanceName":"1"}),"instanceName":"1"}),"instanceName":"1"}),"instanceName":"1"}),"instanceName":"1"}),"instanceName":"1"}),"instanceName":"1"}),"instanceName":"1"});
            var Q1533;
            Q1533=makeQuery(id+"F12.opPattern","COPY",BODY,{"derivedFrom":makeQuery(id+"F11.opPattern","COPY",BODY,{"derivedFrom":makeQuery(id+"F10.opPattern","COPY",BODY,{"derivedFrom":makeQuery(id+"F9.opPattern","COPY",BODY,{"derivedFrom":makeQuery(id+"F8.opPattern","COPY",BODY,{"derivedFrom":makeQuery(id+"F7.opPattern","COPY",BODY,{"derivedFrom":makeQuery(id+"F6.opPattern","COPY",BODY,{"derivedFrom":makeQuery(id+"F5.opPattern","COPY",BODY,{"derivedFrom":makeQuery(id+"F4.opPattern","COPY",BODY,{"derivedFrom":makeQuery(id+"F2.opPattern","COPY",BODY,{"derivedFrom":makeQuery(id+"F1.opRevolve","SWEPT_BODY",BODY,{"disambiguationData":[OSD([sQuery(id+"F0.wireOp",EDGE,"E1")])]}),"instanceName":"1"}),"instanceName":"1"}),"instanceName":"1"}),"instanceName":"1"}),"instanceName":"1"}),"instanceName":"1"}),"instanceName":"1"}),"instanceName":"1"}),"instanceName":"1"}),"instanceName":"1"});
            var Q1534;
            Q1534=makeQuery(id+"F12.opPattern","COPY",BODY,{"derivedFrom":makeQuery(id+"F11.opPattern","COPY",BODY,{"derivedFrom":makeQuery(id+"F10.opPattern","COPY",BODY,{"derivedFrom":makeQuery(id+"F9.opPattern","COPY",BODY,{"derivedFrom":makeQuery(id+"F8.opPattern","COPY",BODY,{"derivedFrom":makeQuery(id+"F7.opPattern","COPY",BODY,{"derivedFrom":makeQuery(id+"F6.opPattern","COPY",BODY,{"derivedFrom":makeQuery(id+"F5.opPattern","COPY",BODY,{"derivedFrom":makeQuery(id+"F4.opPattern","COPY",BODY,{"derivedFrom":makeQuery(id+"F3.opPattern","COPY",BODY,{"derivedFrom":makeQuery(id+"F2.opPattern","COPY",BODY,{"derivedFrom":makeQuery(id+"F1.opRevolve","SWEPT_BODY",BODY,{"disambiguationData":[OSD([sQuery(id+"F0.wireOp",EDGE,"E1")])]}),"instanceName":"1"}),"instanceName":"1"}),"instanceName":"1"}),"instanceName":"1"}),"instanceName":"1"}),"instanceName":"1"}),"instanceName":"1"}),"instanceName":"1"}),"instanceName":"1"}),"instanceName":"1"}),"instanceName":"1"});
            var Q1535;
            Q1535=makeQuery(id+"F13.opPattern","COPY",BODY,{"derivedFrom":makeQuery(id+"F1.opRevolve","SWEPT_BODY",BODY,{"disambiguationData":[OSD([sQuery(id+"F0.wireOp",EDGE,"E1")])]}),"instanceName":"1"});
            var Q1536;
            Q1536=makeQuery(id+"F13.opPattern","COPY",BODY,{"derivedFrom":makeQuery(id+"F2.opPattern","COPY",BODY,{"derivedFrom":makeQuery(id+"F1.opRevolve","SWEPT_BODY",BODY,{"disambiguationData":[OSD([sQuery(id+"F0.wireOp",EDGE,"E1")])]}),"instanceName":"1"}),"instanceName":"1"});
            var Q1537;
            Q1537=makeQuery(id+"F13.opPattern","COPY",BODY,{"derivedFrom":makeQuery(id+"F3.opPattern","COPY",BODY,{"derivedFrom":makeQuery(id+"F2.opPattern","COPY",BODY,{"derivedFrom":makeQuery(id+"F1.opRevolve","SWEPT_BODY",BODY,{"disambiguationData":[OSD([sQuery(id+"F0.wireOp",EDGE,"E1")])]}),"instanceName":"1"}),"instanceName":"1"}),"instanceName":"1"});
            var Q1538;
            Q1538=makeQuery(id+"F13.opPattern","COPY",BODY,{"derivedFrom":makeQuery(id+"F4.opPattern","COPY",BODY,{"derivedFrom":makeQuery(id+"F1.opRevolve","SWEPT_BODY",BODY,{"disambiguationData":[OSD([sQuery(id+"F0.wireOp",EDGE,"E1")])]}),"instanceName":"1"}),"instanceName":"1"});
            var Q1539;
            Q1539=makeQuery(id+"F13.opPattern","COPY",BODY,{"derivedFrom":makeQuery(id+"F4.opPattern","COPY",BODY,{"derivedFrom":makeQuery(id+"F2.opPattern","COPY",BODY,{"derivedFrom":makeQuery(id+"F1.opRevolve","SWEPT_BODY",BODY,{"disambiguationData":[OSD([sQuery(id+"F0.wireOp",EDGE,"E1")])]}),"instanceName":"1"}),"instanceName":"1"}),"instanceName":"1"});
            var Q1540;
            Q1540=makeQuery(id+"F13.opPattern","COPY",BODY,{"derivedFrom":makeQuery(id+"F4.opPattern","COPY",BODY,{"derivedFrom":makeQuery(id+"F3.opPattern","COPY",BODY,{"derivedFrom":makeQuery(id+"F2.opPattern","COPY",BODY,{"derivedFrom":makeQuery(id+"F1.opRevolve","SWEPT_BODY",BODY,{"disambiguationData":[OSD([sQuery(id+"F0.wireOp",EDGE,"E1")])]}),"instanceName":"1"}),"instanceName":"1"}),"instanceName":"1"}),"instanceName":"1"});
            var Q1541;
            Q1541=makeQuery(id+"F13.opPattern","COPY",BODY,{"derivedFrom":makeQuery(id+"F5.opPattern","COPY",BODY,{"derivedFrom":makeQuery(id+"F1.opRevolve","SWEPT_BODY",BODY,{"disambiguationData":[OSD([sQuery(id+"F0.wireOp",EDGE,"E1")])]}),"instanceName":"1"}),"instanceName":"1"});
            var Q1542;
            Q1542=makeQuery(id+"F13.opPattern","COPY",BODY,{"derivedFrom":makeQuery(id+"F5.opPattern","COPY",BODY,{"derivedFrom":makeQuery(id+"F2.opPattern","COPY",BODY,{"derivedFrom":makeQuery(id+"F1.opRevolve","SWEPT_BODY",BODY,{"disambiguationData":[OSD([sQuery(id+"F0.wireOp",EDGE,"E1")])]}),"instanceName":"1"}),"instanceName":"1"}),"instanceName":"1"});
            var Q1543;
            Q1543=makeQuery(id+"F13.opPattern","COPY",BODY,{"derivedFrom":makeQuery(id+"F5.opPattern","COPY",BODY,{"derivedFrom":makeQuery(id+"F3.opPattern","COPY",BODY,{"derivedFrom":makeQuery(id+"F2.opPattern","COPY",BODY,{"derivedFrom":makeQuery(id+"F1.opRevolve","SWEPT_BODY",BODY,{"disambiguationData":[OSD([sQuery(id+"F0.wireOp",EDGE,"E1")])]}),"instanceName":"1"}),"instanceName":"1"}),"instanceName":"1"}),"instanceName":"1"});
            var Q1544;
            Q1544=makeQuery(id+"F13.opPattern","COPY",BODY,{"derivedFrom":makeQuery(id+"F5.opPattern","COPY",BODY,{"derivedFrom":makeQuery(id+"F4.opPattern","COPY",BODY,{"derivedFrom":makeQuery(id+"F1.opRevolve","SWEPT_BODY",BODY,{"disambiguationData":[OSD([sQuery(id+"F0.wireOp",EDGE,"E1")])]}),"instanceName":"1"}),"instanceName":"1"}),"instanceName":"1"});
            var Q1545;
            Q1545=makeQuery(id+"F13.opPattern","COPY",BODY,{"derivedFrom":makeQuery(id+"F5.opPattern","COPY",BODY,{"derivedFrom":makeQuery(id+"F4.opPattern","COPY",BODY,{"derivedFrom":makeQuery(id+"F2.opPattern","COPY",BODY,{"derivedFrom":makeQuery(id+"F1.opRevolve","SWEPT_BODY",BODY,{"disambiguationData":[OSD([sQuery(id+"F0.wireOp",EDGE,"E1")])]}),"instanceName":"1"}),"instanceName":"1"}),"instanceName":"1"}),"instanceName":"1"});
            var Q1546;
            Q1546=makeQuery(id+"F13.opPattern","COPY",BODY,{"derivedFrom":makeQuery(id+"F5.opPattern","COPY",BODY,{"derivedFrom":makeQuery(id+"F4.opPattern","COPY",BODY,{"derivedFrom":makeQuery(id+"F3.opPattern","COPY",BODY,{"derivedFrom":makeQuery(id+"F2.opPattern","COPY",BODY,{"derivedFrom":makeQuery(id+"F1.opRevolve","SWEPT_BODY",BODY,{"disambiguationData":[OSD([sQuery(id+"F0.wireOp",EDGE,"E1")])]}),"instanceName":"1"}),"instanceName":"1"}),"instanceName":"1"}),"instanceName":"1"}),"instanceName":"1"});
            var Q1547;
            Q1547=makeQuery(id+"F13.opPattern","COPY",BODY,{"derivedFrom":makeQuery(id+"F6.opPattern","COPY",BODY,{"derivedFrom":makeQuery(id+"F1.opRevolve","SWEPT_BODY",BODY,{"disambiguationData":[OSD([sQuery(id+"F0.wireOp",EDGE,"E1")])]}),"instanceName":"1"}),"instanceName":"1"});
            var Q1548;
            Q1548=makeQuery(id+"F13.opPattern","COPY",BODY,{"derivedFrom":makeQuery(id+"F6.opPattern","COPY",BODY,{"derivedFrom":makeQuery(id+"F2.opPattern","COPY",BODY,{"derivedFrom":makeQuery(id+"F1.opRevolve","SWEPT_BODY",BODY,{"disambiguationData":[OSD([sQuery(id+"F0.wireOp",EDGE,"E1")])]}),"instanceName":"1"}),"instanceName":"1"}),"instanceName":"1"});
            var Q1549;
            Q1549=makeQuery(id+"F13.opPattern","COPY",BODY,{"derivedFrom":makeQuery(id+"F6.opPattern","COPY",BODY,{"derivedFrom":makeQuery(id+"F3.opPattern","COPY",BODY,{"derivedFrom":makeQuery(id+"F2.opPattern","COPY",BODY,{"derivedFrom":makeQuery(id+"F1.opRevolve","SWEPT_BODY",BODY,{"disambiguationData":[OSD([sQuery(id+"F0.wireOp",EDGE,"E1")])]}),"instanceName":"1"}),"instanceName":"1"}),"instanceName":"1"}),"instanceName":"1"});
            var Q1550;
            Q1550=makeQuery(id+"F13.opPattern","COPY",BODY,{"derivedFrom":makeQuery(id+"F6.opPattern","COPY",BODY,{"derivedFrom":makeQuery(id+"F4.opPattern","COPY",BODY,{"derivedFrom":makeQuery(id+"F1.opRevolve","SWEPT_BODY",BODY,{"disambiguationData":[OSD([sQuery(id+"F0.wireOp",EDGE,"E1")])]}),"instanceName":"1"}),"instanceName":"1"}),"instanceName":"1"});
            var Q1551;
            Q1551=makeQuery(id+"F13.opPattern","COPY",BODY,{"derivedFrom":makeQuery(id+"F6.opPattern","COPY",BODY,{"derivedFrom":makeQuery(id+"F4.opPattern","COPY",BODY,{"derivedFrom":makeQuery(id+"F2.opPattern","COPY",BODY,{"derivedFrom":makeQuery(id+"F1.opRevolve","SWEPT_BODY",BODY,{"disambiguationData":[OSD([sQuery(id+"F0.wireOp",EDGE,"E1")])]}),"instanceName":"1"}),"instanceName":"1"}),"instanceName":"1"}),"instanceName":"1"});
            var Q1552;
            Q1552=makeQuery(id+"F13.opPattern","COPY",BODY,{"derivedFrom":makeQuery(id+"F6.opPattern","COPY",BODY,{"derivedFrom":makeQuery(id+"F4.opPattern","COPY",BODY,{"derivedFrom":makeQuery(id+"F3.opPattern","COPY",BODY,{"derivedFrom":makeQuery(id+"F2.opPattern","COPY",BODY,{"derivedFrom":makeQuery(id+"F1.opRevolve","SWEPT_BODY",BODY,{"disambiguationData":[OSD([sQuery(id+"F0.wireOp",EDGE,"E1")])]}),"instanceName":"1"}),"instanceName":"1"}),"instanceName":"1"}),"instanceName":"1"}),"instanceName":"1"});
            var Q1553;
            Q1553=makeQuery(id+"F13.opPattern","COPY",BODY,{"derivedFrom":makeQuery(id+"F6.opPattern","COPY",BODY,{"derivedFrom":makeQuery(id+"F5.opPattern","COPY",BODY,{"derivedFrom":makeQuery(id+"F1.opRevolve","SWEPT_BODY",BODY,{"disambiguationData":[OSD([sQuery(id+"F0.wireOp",EDGE,"E1")])]}),"instanceName":"1"}),"instanceName":"1"}),"instanceName":"1"});
            var Q1554;
            Q1554=makeQuery(id+"F13.opPattern","COPY",BODY,{"derivedFrom":makeQuery(id+"F6.opPattern","COPY",BODY,{"derivedFrom":makeQuery(id+"F5.opPattern","COPY",BODY,{"derivedFrom":makeQuery(id+"F2.opPattern","COPY",BODY,{"derivedFrom":makeQuery(id+"F1.opRevolve","SWEPT_BODY",BODY,{"disambiguationData":[OSD([sQuery(id+"F0.wireOp",EDGE,"E1")])]}),"instanceName":"1"}),"instanceName":"1"}),"instanceName":"1"}),"instanceName":"1"});
            var Q1555;
            Q1555=makeQuery(id+"F13.opPattern","COPY",BODY,{"derivedFrom":makeQuery(id+"F6.opPattern","COPY",BODY,{"derivedFrom":makeQuery(id+"F5.opPattern","COPY",BODY,{"derivedFrom":makeQuery(id+"F3.opPattern","COPY",BODY,{"derivedFrom":makeQuery(id+"F2.opPattern","COPY",BODY,{"derivedFrom":makeQuery(id+"F1.opRevolve","SWEPT_BODY",BODY,{"disambiguationData":[OSD([sQuery(id+"F0.wireOp",EDGE,"E1")])]}),"instanceName":"1"}),"instanceName":"1"}),"instanceName":"1"}),"instanceName":"1"}),"instanceName":"1"});
            var Q1556;
            Q1556=makeQuery(id+"F13.opPattern","COPY",BODY,{"derivedFrom":makeQuery(id+"F6.opPattern","COPY",BODY,{"derivedFrom":makeQuery(id+"F5.opPattern","COPY",BODY,{"derivedFrom":makeQuery(id+"F4.opPattern","COPY",BODY,{"derivedFrom":makeQuery(id+"F1.opRevolve","SWEPT_BODY",BODY,{"disambiguationData":[OSD([sQuery(id+"F0.wireOp",EDGE,"E1")])]}),"instanceName":"1"}),"instanceName":"1"}),"instanceName":"1"}),"instanceName":"1"});
            var Q1557;
            Q1557=makeQuery(id+"F13.opPattern","COPY",BODY,{"derivedFrom":makeQuery(id+"F6.opPattern","COPY",BODY,{"derivedFrom":makeQuery(id+"F5.opPattern","COPY",BODY,{"derivedFrom":makeQuery(id+"F4.opPattern","COPY",BODY,{"derivedFrom":makeQuery(id+"F2.opPattern","COPY",BODY,{"derivedFrom":makeQuery(id+"F1.opRevolve","SWEPT_BODY",BODY,{"disambiguationData":[OSD([sQuery(id+"F0.wireOp",EDGE,"E1")])]}),"instanceName":"1"}),"instanceName":"1"}),"instanceName":"1"}),"instanceName":"1"}),"instanceName":"1"});
            var Q1558;
            Q1558=makeQuery(id+"F13.opPattern","COPY",BODY,{"derivedFrom":makeQuery(id+"F6.opPattern","COPY",BODY,{"derivedFrom":makeQuery(id+"F5.opPattern","COPY",BODY,{"derivedFrom":makeQuery(id+"F4.opPattern","COPY",BODY,{"derivedFrom":makeQuery(id+"F3.opPattern","COPY",BODY,{"derivedFrom":makeQuery(id+"F2.opPattern","COPY",BODY,{"derivedFrom":makeQuery(id+"F1.opRevolve","SWEPT_BODY",BODY,{"disambiguationData":[OSD([sQuery(id+"F0.wireOp",EDGE,"E1")])]}),"instanceName":"1"}),"instanceName":"1"}),"instanceName":"1"}),"instanceName":"1"}),"instanceName":"1"}),"instanceName":"1"});
            var Q1559;
            Q1559=makeQuery(id+"F13.opPattern","COPY",BODY,{"derivedFrom":makeQuery(id+"F7.opPattern","COPY",BODY,{"derivedFrom":makeQuery(id+"F1.opRevolve","SWEPT_BODY",BODY,{"disambiguationData":[OSD([sQuery(id+"F0.wireOp",EDGE,"E1")])]}),"instanceName":"1"}),"instanceName":"1"});
            var Q1560;
            Q1560=makeQuery(id+"F13.opPattern","COPY",BODY,{"derivedFrom":makeQuery(id+"F7.opPattern","COPY",BODY,{"derivedFrom":makeQuery(id+"F2.opPattern","COPY",BODY,{"derivedFrom":makeQuery(id+"F1.opRevolve","SWEPT_BODY",BODY,{"disambiguationData":[OSD([sQuery(id+"F0.wireOp",EDGE,"E1")])]}),"instanceName":"1"}),"instanceName":"1"}),"instanceName":"1"});
            var Q1561;
            Q1561=makeQuery(id+"F13.opPattern","COPY",BODY,{"derivedFrom":makeQuery(id+"F7.opPattern","COPY",BODY,{"derivedFrom":makeQuery(id+"F3.opPattern","COPY",BODY,{"derivedFrom":makeQuery(id+"F2.opPattern","COPY",BODY,{"derivedFrom":makeQuery(id+"F1.opRevolve","SWEPT_BODY",BODY,{"disambiguationData":[OSD([sQuery(id+"F0.wireOp",EDGE,"E1")])]}),"instanceName":"1"}),"instanceName":"1"}),"instanceName":"1"}),"instanceName":"1"});
            var Q1562;
            Q1562=makeQuery(id+"F13.opPattern","COPY",BODY,{"derivedFrom":makeQuery(id+"F7.opPattern","COPY",BODY,{"derivedFrom":makeQuery(id+"F4.opPattern","COPY",BODY,{"derivedFrom":makeQuery(id+"F1.opRevolve","SWEPT_BODY",BODY,{"disambiguationData":[OSD([sQuery(id+"F0.wireOp",EDGE,"E1")])]}),"instanceName":"1"}),"instanceName":"1"}),"instanceName":"1"});
            var Q1563;
            Q1563=makeQuery(id+"F13.opPattern","COPY",BODY,{"derivedFrom":makeQuery(id+"F7.opPattern","COPY",BODY,{"derivedFrom":makeQuery(id+"F4.opPattern","COPY",BODY,{"derivedFrom":makeQuery(id+"F2.opPattern","COPY",BODY,{"derivedFrom":makeQuery(id+"F1.opRevolve","SWEPT_BODY",BODY,{"disambiguationData":[OSD([sQuery(id+"F0.wireOp",EDGE,"E1")])]}),"instanceName":"1"}),"instanceName":"1"}),"instanceName":"1"}),"instanceName":"1"});
            var Q1564;
            Q1564=makeQuery(id+"F13.opPattern","COPY",BODY,{"derivedFrom":makeQuery(id+"F7.opPattern","COPY",BODY,{"derivedFrom":makeQuery(id+"F4.opPattern","COPY",BODY,{"derivedFrom":makeQuery(id+"F3.opPattern","COPY",BODY,{"derivedFrom":makeQuery(id+"F2.opPattern","COPY",BODY,{"derivedFrom":makeQuery(id+"F1.opRevolve","SWEPT_BODY",BODY,{"disambiguationData":[OSD([sQuery(id+"F0.wireOp",EDGE,"E1")])]}),"instanceName":"1"}),"instanceName":"1"}),"instanceName":"1"}),"instanceName":"1"}),"instanceName":"1"});
            var Q1565;
            Q1565=makeQuery(id+"F13.opPattern","COPY",BODY,{"derivedFrom":makeQuery(id+"F7.opPattern","COPY",BODY,{"derivedFrom":makeQuery(id+"F5.opPattern","COPY",BODY,{"derivedFrom":makeQuery(id+"F1.opRevolve","SWEPT_BODY",BODY,{"disambiguationData":[OSD([sQuery(id+"F0.wireOp",EDGE,"E1")])]}),"instanceName":"1"}),"instanceName":"1"}),"instanceName":"1"});
            var Q1566;
            Q1566=makeQuery(id+"F13.opPattern","COPY",BODY,{"derivedFrom":makeQuery(id+"F7.opPattern","COPY",BODY,{"derivedFrom":makeQuery(id+"F5.opPattern","COPY",BODY,{"derivedFrom":makeQuery(id+"F2.opPattern","COPY",BODY,{"derivedFrom":makeQuery(id+"F1.opRevolve","SWEPT_BODY",BODY,{"disambiguationData":[OSD([sQuery(id+"F0.wireOp",EDGE,"E1")])]}),"instanceName":"1"}),"instanceName":"1"}),"instanceName":"1"}),"instanceName":"1"});
            var Q1567;
            Q1567=makeQuery(id+"F13.opPattern","COPY",BODY,{"derivedFrom":makeQuery(id+"F7.opPattern","COPY",BODY,{"derivedFrom":makeQuery(id+"F5.opPattern","COPY",BODY,{"derivedFrom":makeQuery(id+"F3.opPattern","COPY",BODY,{"derivedFrom":makeQuery(id+"F2.opPattern","COPY",BODY,{"derivedFrom":makeQuery(id+"F1.opRevolve","SWEPT_BODY",BODY,{"disambiguationData":[OSD([sQuery(id+"F0.wireOp",EDGE,"E1")])]}),"instanceName":"1"}),"instanceName":"1"}),"instanceName":"1"}),"instanceName":"1"}),"instanceName":"1"});
            var Q1568;
            Q1568=makeQuery(id+"F13.opPattern","COPY",BODY,{"derivedFrom":makeQuery(id+"F7.opPattern","COPY",BODY,{"derivedFrom":makeQuery(id+"F5.opPattern","COPY",BODY,{"derivedFrom":makeQuery(id+"F4.opPattern","COPY",BODY,{"derivedFrom":makeQuery(id+"F1.opRevolve","SWEPT_BODY",BODY,{"disambiguationData":[OSD([sQuery(id+"F0.wireOp",EDGE,"E1")])]}),"instanceName":"1"}),"instanceName":"1"}),"instanceName":"1"}),"instanceName":"1"});
            var Q1569;
            Q1569=makeQuery(id+"F13.opPattern","COPY",BODY,{"derivedFrom":makeQuery(id+"F7.opPattern","COPY",BODY,{"derivedFrom":makeQuery(id+"F5.opPattern","COPY",BODY,{"derivedFrom":makeQuery(id+"F4.opPattern","COPY",BODY,{"derivedFrom":makeQuery(id+"F2.opPattern","COPY",BODY,{"derivedFrom":makeQuery(id+"F1.opRevolve","SWEPT_BODY",BODY,{"disambiguationData":[OSD([sQuery(id+"F0.wireOp",EDGE,"E1")])]}),"instanceName":"1"}),"instanceName":"1"}),"instanceName":"1"}),"instanceName":"1"}),"instanceName":"1"});
            var Q1570;
            Q1570=makeQuery(id+"F13.opPattern","COPY",BODY,{"derivedFrom":makeQuery(id+"F7.opPattern","COPY",BODY,{"derivedFrom":makeQuery(id+"F5.opPattern","COPY",BODY,{"derivedFrom":makeQuery(id+"F4.opPattern","COPY",BODY,{"derivedFrom":makeQuery(id+"F3.opPattern","COPY",BODY,{"derivedFrom":makeQuery(id+"F2.opPattern","COPY",BODY,{"derivedFrom":makeQuery(id+"F1.opRevolve","SWEPT_BODY",BODY,{"disambiguationData":[OSD([sQuery(id+"F0.wireOp",EDGE,"E1")])]}),"instanceName":"1"}),"instanceName":"1"}),"instanceName":"1"}),"instanceName":"1"}),"instanceName":"1"}),"instanceName":"1"});
            var Q1571;
            Q1571=makeQuery(id+"F13.opPattern","COPY",BODY,{"derivedFrom":makeQuery(id+"F7.opPattern","COPY",BODY,{"derivedFrom":makeQuery(id+"F6.opPattern","COPY",BODY,{"derivedFrom":makeQuery(id+"F1.opRevolve","SWEPT_BODY",BODY,{"disambiguationData":[OSD([sQuery(id+"F0.wireOp",EDGE,"E1")])]}),"instanceName":"1"}),"instanceName":"1"}),"instanceName":"1"});
            var Q1572;
            Q1572=makeQuery(id+"F13.opPattern","COPY",BODY,{"derivedFrom":makeQuery(id+"F7.opPattern","COPY",BODY,{"derivedFrom":makeQuery(id+"F6.opPattern","COPY",BODY,{"derivedFrom":makeQuery(id+"F2.opPattern","COPY",BODY,{"derivedFrom":makeQuery(id+"F1.opRevolve","SWEPT_BODY",BODY,{"disambiguationData":[OSD([sQuery(id+"F0.wireOp",EDGE,"E1")])]}),"instanceName":"1"}),"instanceName":"1"}),"instanceName":"1"}),"instanceName":"1"});
            var Q1573;
            Q1573=makeQuery(id+"F13.opPattern","COPY",BODY,{"derivedFrom":makeQuery(id+"F7.opPattern","COPY",BODY,{"derivedFrom":makeQuery(id+"F6.opPattern","COPY",BODY,{"derivedFrom":makeQuery(id+"F3.opPattern","COPY",BODY,{"derivedFrom":makeQuery(id+"F2.opPattern","COPY",BODY,{"derivedFrom":makeQuery(id+"F1.opRevolve","SWEPT_BODY",BODY,{"disambiguationData":[OSD([sQuery(id+"F0.wireOp",EDGE,"E1")])]}),"instanceName":"1"}),"instanceName":"1"}),"instanceName":"1"}),"instanceName":"1"}),"instanceName":"1"});
            var Q1574;
            Q1574=makeQuery(id+"F13.opPattern","COPY",BODY,{"derivedFrom":makeQuery(id+"F7.opPattern","COPY",BODY,{"derivedFrom":makeQuery(id+"F6.opPattern","COPY",BODY,{"derivedFrom":makeQuery(id+"F4.opPattern","COPY",BODY,{"derivedFrom":makeQuery(id+"F1.opRevolve","SWEPT_BODY",BODY,{"disambiguationData":[OSD([sQuery(id+"F0.wireOp",EDGE,"E1")])]}),"instanceName":"1"}),"instanceName":"1"}),"instanceName":"1"}),"instanceName":"1"});
            var Q1575;
            Q1575=makeQuery(id+"F13.opPattern","COPY",BODY,{"derivedFrom":makeQuery(id+"F7.opPattern","COPY",BODY,{"derivedFrom":makeQuery(id+"F6.opPattern","COPY",BODY,{"derivedFrom":makeQuery(id+"F4.opPattern","COPY",BODY,{"derivedFrom":makeQuery(id+"F2.opPattern","COPY",BODY,{"derivedFrom":makeQuery(id+"F1.opRevolve","SWEPT_BODY",BODY,{"disambiguationData":[OSD([sQuery(id+"F0.wireOp",EDGE,"E1")])]}),"instanceName":"1"}),"instanceName":"1"}),"instanceName":"1"}),"instanceName":"1"}),"instanceName":"1"});
            var Q1576;
            Q1576=makeQuery(id+"F13.opPattern","COPY",BODY,{"derivedFrom":makeQuery(id+"F7.opPattern","COPY",BODY,{"derivedFrom":makeQuery(id+"F6.opPattern","COPY",BODY,{"derivedFrom":makeQuery(id+"F4.opPattern","COPY",BODY,{"derivedFrom":makeQuery(id+"F3.opPattern","COPY",BODY,{"derivedFrom":makeQuery(id+"F2.opPattern","COPY",BODY,{"derivedFrom":makeQuery(id+"F1.opRevolve","SWEPT_BODY",BODY,{"disambiguationData":[OSD([sQuery(id+"F0.wireOp",EDGE,"E1")])]}),"instanceName":"1"}),"instanceName":"1"}),"instanceName":"1"}),"instanceName":"1"}),"instanceName":"1"}),"instanceName":"1"});
            var Q1577;
            Q1577=makeQuery(id+"F13.opPattern","COPY",BODY,{"derivedFrom":makeQuery(id+"F7.opPattern","COPY",BODY,{"derivedFrom":makeQuery(id+"F6.opPattern","COPY",BODY,{"derivedFrom":makeQuery(id+"F5.opPattern","COPY",BODY,{"derivedFrom":makeQuery(id+"F1.opRevolve","SWEPT_BODY",BODY,{"disambiguationData":[OSD([sQuery(id+"F0.wireOp",EDGE,"E1")])]}),"instanceName":"1"}),"instanceName":"1"}),"instanceName":"1"}),"instanceName":"1"});
            var Q1578;
            Q1578=makeQuery(id+"F13.opPattern","COPY",BODY,{"derivedFrom":makeQuery(id+"F7.opPattern","COPY",BODY,{"derivedFrom":makeQuery(id+"F6.opPattern","COPY",BODY,{"derivedFrom":makeQuery(id+"F5.opPattern","COPY",BODY,{"derivedFrom":makeQuery(id+"F2.opPattern","COPY",BODY,{"derivedFrom":makeQuery(id+"F1.opRevolve","SWEPT_BODY",BODY,{"disambiguationData":[OSD([sQuery(id+"F0.wireOp",EDGE,"E1")])]}),"instanceName":"1"}),"instanceName":"1"}),"instanceName":"1"}),"instanceName":"1"}),"instanceName":"1"});
            var Q1579;
            Q1579=makeQuery(id+"F13.opPattern","COPY",BODY,{"derivedFrom":makeQuery(id+"F7.opPattern","COPY",BODY,{"derivedFrom":makeQuery(id+"F6.opPattern","COPY",BODY,{"derivedFrom":makeQuery(id+"F5.opPattern","COPY",BODY,{"derivedFrom":makeQuery(id+"F3.opPattern","COPY",BODY,{"derivedFrom":makeQuery(id+"F2.opPattern","COPY",BODY,{"derivedFrom":makeQuery(id+"F1.opRevolve","SWEPT_BODY",BODY,{"disambiguationData":[OSD([sQuery(id+"F0.wireOp",EDGE,"E1")])]}),"instanceName":"1"}),"instanceName":"1"}),"instanceName":"1"}),"instanceName":"1"}),"instanceName":"1"}),"instanceName":"1"});
            var Q1580;
            Q1580=makeQuery(id+"F13.opPattern","COPY",BODY,{"derivedFrom":makeQuery(id+"F7.opPattern","COPY",BODY,{"derivedFrom":makeQuery(id+"F6.opPattern","COPY",BODY,{"derivedFrom":makeQuery(id+"F5.opPattern","COPY",BODY,{"derivedFrom":makeQuery(id+"F4.opPattern","COPY",BODY,{"derivedFrom":makeQuery(id+"F1.opRevolve","SWEPT_BODY",BODY,{"disambiguationData":[OSD([sQuery(id+"F0.wireOp",EDGE,"E1")])]}),"instanceName":"1"}),"instanceName":"1"}),"instanceName":"1"}),"instanceName":"1"}),"instanceName":"1"});
            var Q1581;
            Q1581=makeQuery(id+"F13.opPattern","COPY",BODY,{"derivedFrom":makeQuery(id+"F7.opPattern","COPY",BODY,{"derivedFrom":makeQuery(id+"F6.opPattern","COPY",BODY,{"derivedFrom":makeQuery(id+"F5.opPattern","COPY",BODY,{"derivedFrom":makeQuery(id+"F4.opPattern","COPY",BODY,{"derivedFrom":makeQuery(id+"F2.opPattern","COPY",BODY,{"derivedFrom":makeQuery(id+"F1.opRevolve","SWEPT_BODY",BODY,{"disambiguationData":[OSD([sQuery(id+"F0.wireOp",EDGE,"E1")])]}),"instanceName":"1"}),"instanceName":"1"}),"instanceName":"1"}),"instanceName":"1"}),"instanceName":"1"}),"instanceName":"1"});
            var Q1582;
            Q1582=makeQuery(id+"F13.opPattern","COPY",BODY,{"derivedFrom":makeQuery(id+"F7.opPattern","COPY",BODY,{"derivedFrom":makeQuery(id+"F6.opPattern","COPY",BODY,{"derivedFrom":makeQuery(id+"F5.opPattern","COPY",BODY,{"derivedFrom":makeQuery(id+"F4.opPattern","COPY",BODY,{"derivedFrom":makeQuery(id+"F3.opPattern","COPY",BODY,{"derivedFrom":makeQuery(id+"F2.opPattern","COPY",BODY,{"derivedFrom":makeQuery(id+"F1.opRevolve","SWEPT_BODY",BODY,{"disambiguationData":[OSD([sQuery(id+"F0.wireOp",EDGE,"E1")])]}),"instanceName":"1"}),"instanceName":"1"}),"instanceName":"1"}),"instanceName":"1"}),"instanceName":"1"}),"instanceName":"1"}),"instanceName":"1"});
            var Q1583;
            Q1583=makeQuery(id+"F13.opPattern","COPY",BODY,{"derivedFrom":makeQuery(id+"F8.opPattern","COPY",BODY,{"derivedFrom":makeQuery(id+"F1.opRevolve","SWEPT_BODY",BODY,{"disambiguationData":[OSD([sQuery(id+"F0.wireOp",EDGE,"E1")])]}),"instanceName":"1"}),"instanceName":"1"});
            var Q1584;
            Q1584=makeQuery(id+"F13.opPattern","COPY",BODY,{"derivedFrom":makeQuery(id+"F8.opPattern","COPY",BODY,{"derivedFrom":makeQuery(id+"F2.opPattern","COPY",BODY,{"derivedFrom":makeQuery(id+"F1.opRevolve","SWEPT_BODY",BODY,{"disambiguationData":[OSD([sQuery(id+"F0.wireOp",EDGE,"E1")])]}),"instanceName":"1"}),"instanceName":"1"}),"instanceName":"1"});
            var Q1585;
            Q1585=makeQuery(id+"F13.opPattern","COPY",BODY,{"derivedFrom":makeQuery(id+"F8.opPattern","COPY",BODY,{"derivedFrom":makeQuery(id+"F3.opPattern","COPY",BODY,{"derivedFrom":makeQuery(id+"F2.opPattern","COPY",BODY,{"derivedFrom":makeQuery(id+"F1.opRevolve","SWEPT_BODY",BODY,{"disambiguationData":[OSD([sQuery(id+"F0.wireOp",EDGE,"E1")])]}),"instanceName":"1"}),"instanceName":"1"}),"instanceName":"1"}),"instanceName":"1"});
            var Q1586;
            Q1586=makeQuery(id+"F13.opPattern","COPY",BODY,{"derivedFrom":makeQuery(id+"F8.opPattern","COPY",BODY,{"derivedFrom":makeQuery(id+"F4.opPattern","COPY",BODY,{"derivedFrom":makeQuery(id+"F1.opRevolve","SWEPT_BODY",BODY,{"disambiguationData":[OSD([sQuery(id+"F0.wireOp",EDGE,"E1")])]}),"instanceName":"1"}),"instanceName":"1"}),"instanceName":"1"});
            var Q1587;
            Q1587=makeQuery(id+"F13.opPattern","COPY",BODY,{"derivedFrom":makeQuery(id+"F8.opPattern","COPY",BODY,{"derivedFrom":makeQuery(id+"F4.opPattern","COPY",BODY,{"derivedFrom":makeQuery(id+"F2.opPattern","COPY",BODY,{"derivedFrom":makeQuery(id+"F1.opRevolve","SWEPT_BODY",BODY,{"disambiguationData":[OSD([sQuery(id+"F0.wireOp",EDGE,"E1")])]}),"instanceName":"1"}),"instanceName":"1"}),"instanceName":"1"}),"instanceName":"1"});
            var Q1588;
            Q1588=makeQuery(id+"F13.opPattern","COPY",BODY,{"derivedFrom":makeQuery(id+"F8.opPattern","COPY",BODY,{"derivedFrom":makeQuery(id+"F4.opPattern","COPY",BODY,{"derivedFrom":makeQuery(id+"F3.opPattern","COPY",BODY,{"derivedFrom":makeQuery(id+"F2.opPattern","COPY",BODY,{"derivedFrom":makeQuery(id+"F1.opRevolve","SWEPT_BODY",BODY,{"disambiguationData":[OSD([sQuery(id+"F0.wireOp",EDGE,"E1")])]}),"instanceName":"1"}),"instanceName":"1"}),"instanceName":"1"}),"instanceName":"1"}),"instanceName":"1"});
            var Q1589;
            Q1589=makeQuery(id+"F13.opPattern","COPY",BODY,{"derivedFrom":makeQuery(id+"F8.opPattern","COPY",BODY,{"derivedFrom":makeQuery(id+"F5.opPattern","COPY",BODY,{"derivedFrom":makeQuery(id+"F1.opRevolve","SWEPT_BODY",BODY,{"disambiguationData":[OSD([sQuery(id+"F0.wireOp",EDGE,"E1")])]}),"instanceName":"1"}),"instanceName":"1"}),"instanceName":"1"});
            var Q1590;
            Q1590=makeQuery(id+"F13.opPattern","COPY",BODY,{"derivedFrom":makeQuery(id+"F8.opPattern","COPY",BODY,{"derivedFrom":makeQuery(id+"F5.opPattern","COPY",BODY,{"derivedFrom":makeQuery(id+"F2.opPattern","COPY",BODY,{"derivedFrom":makeQuery(id+"F1.opRevolve","SWEPT_BODY",BODY,{"disambiguationData":[OSD([sQuery(id+"F0.wireOp",EDGE,"E1")])]}),"instanceName":"1"}),"instanceName":"1"}),"instanceName":"1"}),"instanceName":"1"});
            var Q1591;
            Q1591=makeQuery(id+"F13.opPattern","COPY",BODY,{"derivedFrom":makeQuery(id+"F8.opPattern","COPY",BODY,{"derivedFrom":makeQuery(id+"F5.opPattern","COPY",BODY,{"derivedFrom":makeQuery(id+"F3.opPattern","COPY",BODY,{"derivedFrom":makeQuery(id+"F2.opPattern","COPY",BODY,{"derivedFrom":makeQuery(id+"F1.opRevolve","SWEPT_BODY",BODY,{"disambiguationData":[OSD([sQuery(id+"F0.wireOp",EDGE,"E1")])]}),"instanceName":"1"}),"instanceName":"1"}),"instanceName":"1"}),"instanceName":"1"}),"instanceName":"1"});
            var Q1592;
            Q1592=makeQuery(id+"F13.opPattern","COPY",BODY,{"derivedFrom":makeQuery(id+"F8.opPattern","COPY",BODY,{"derivedFrom":makeQuery(id+"F5.opPattern","COPY",BODY,{"derivedFrom":makeQuery(id+"F4.opPattern","COPY",BODY,{"derivedFrom":makeQuery(id+"F1.opRevolve","SWEPT_BODY",BODY,{"disambiguationData":[OSD([sQuery(id+"F0.wireOp",EDGE,"E1")])]}),"instanceName":"1"}),"instanceName":"1"}),"instanceName":"1"}),"instanceName":"1"});
            var Q1593;
            Q1593=makeQuery(id+"F13.opPattern","COPY",BODY,{"derivedFrom":makeQuery(id+"F8.opPattern","COPY",BODY,{"derivedFrom":makeQuery(id+"F5.opPattern","COPY",BODY,{"derivedFrom":makeQuery(id+"F4.opPattern","COPY",BODY,{"derivedFrom":makeQuery(id+"F2.opPattern","COPY",BODY,{"derivedFrom":makeQuery(id+"F1.opRevolve","SWEPT_BODY",BODY,{"disambiguationData":[OSD([sQuery(id+"F0.wireOp",EDGE,"E1")])]}),"instanceName":"1"}),"instanceName":"1"}),"instanceName":"1"}),"instanceName":"1"}),"instanceName":"1"});
            var Q1594;
            Q1594=makeQuery(id+"F13.opPattern","COPY",BODY,{"derivedFrom":makeQuery(id+"F8.opPattern","COPY",BODY,{"derivedFrom":makeQuery(id+"F5.opPattern","COPY",BODY,{"derivedFrom":makeQuery(id+"F4.opPattern","COPY",BODY,{"derivedFrom":makeQuery(id+"F3.opPattern","COPY",BODY,{"derivedFrom":makeQuery(id+"F2.opPattern","COPY",BODY,{"derivedFrom":makeQuery(id+"F1.opRevolve","SWEPT_BODY",BODY,{"disambiguationData":[OSD([sQuery(id+"F0.wireOp",EDGE,"E1")])]}),"instanceName":"1"}),"instanceName":"1"}),"instanceName":"1"}),"instanceName":"1"}),"instanceName":"1"}),"instanceName":"1"});
            var Q1595;
            Q1595=makeQuery(id+"F13.opPattern","COPY",BODY,{"derivedFrom":makeQuery(id+"F8.opPattern","COPY",BODY,{"derivedFrom":makeQuery(id+"F6.opPattern","COPY",BODY,{"derivedFrom":makeQuery(id+"F1.opRevolve","SWEPT_BODY",BODY,{"disambiguationData":[OSD([sQuery(id+"F0.wireOp",EDGE,"E1")])]}),"instanceName":"1"}),"instanceName":"1"}),"instanceName":"1"});
            var Q1596;
            Q1596=makeQuery(id+"F13.opPattern","COPY",BODY,{"derivedFrom":makeQuery(id+"F8.opPattern","COPY",BODY,{"derivedFrom":makeQuery(id+"F6.opPattern","COPY",BODY,{"derivedFrom":makeQuery(id+"F2.opPattern","COPY",BODY,{"derivedFrom":makeQuery(id+"F1.opRevolve","SWEPT_BODY",BODY,{"disambiguationData":[OSD([sQuery(id+"F0.wireOp",EDGE,"E1")])]}),"instanceName":"1"}),"instanceName":"1"}),"instanceName":"1"}),"instanceName":"1"});
            var Q1597;
            Q1597=makeQuery(id+"F13.opPattern","COPY",BODY,{"derivedFrom":makeQuery(id+"F8.opPattern","COPY",BODY,{"derivedFrom":makeQuery(id+"F6.opPattern","COPY",BODY,{"derivedFrom":makeQuery(id+"F3.opPattern","COPY",BODY,{"derivedFrom":makeQuery(id+"F2.opPattern","COPY",BODY,{"derivedFrom":makeQuery(id+"F1.opRevolve","SWEPT_BODY",BODY,{"disambiguationData":[OSD([sQuery(id+"F0.wireOp",EDGE,"E1")])]}),"instanceName":"1"}),"instanceName":"1"}),"instanceName":"1"}),"instanceName":"1"}),"instanceName":"1"});
            var Q1598;
            Q1598=makeQuery(id+"F13.opPattern","COPY",BODY,{"derivedFrom":makeQuery(id+"F8.opPattern","COPY",BODY,{"derivedFrom":makeQuery(id+"F6.opPattern","COPY",BODY,{"derivedFrom":makeQuery(id+"F4.opPattern","COPY",BODY,{"derivedFrom":makeQuery(id+"F1.opRevolve","SWEPT_BODY",BODY,{"disambiguationData":[OSD([sQuery(id+"F0.wireOp",EDGE,"E1")])]}),"instanceName":"1"}),"instanceName":"1"}),"instanceName":"1"}),"instanceName":"1"});
            var Q1599;
            Q1599=makeQuery(id+"F13.opPattern","COPY",BODY,{"derivedFrom":makeQuery(id+"F8.opPattern","COPY",BODY,{"derivedFrom":makeQuery(id+"F6.opPattern","COPY",BODY,{"derivedFrom":makeQuery(id+"F4.opPattern","COPY",BODY,{"derivedFrom":makeQuery(id+"F2.opPattern","COPY",BODY,{"derivedFrom":makeQuery(id+"F1.opRevolve","SWEPT_BODY",BODY,{"disambiguationData":[OSD([sQuery(id+"F0.wireOp",EDGE,"E1")])]}),"instanceName":"1"}),"instanceName":"1"}),"instanceName":"1"}),"instanceName":"1"}),"instanceName":"1"});
            var Q1600;
            Q1600=makeQuery(id+"F13.opPattern","COPY",BODY,{"derivedFrom":makeQuery(id+"F8.opPattern","COPY",BODY,{"derivedFrom":makeQuery(id+"F6.opPattern","COPY",BODY,{"derivedFrom":makeQuery(id+"F4.opPattern","COPY",BODY,{"derivedFrom":makeQuery(id+"F3.opPattern","COPY",BODY,{"derivedFrom":makeQuery(id+"F2.opPattern","COPY",BODY,{"derivedFrom":makeQuery(id+"F1.opRevolve","SWEPT_BODY",BODY,{"disambiguationData":[OSD([sQuery(id+"F0.wireOp",EDGE,"E1")])]}),"instanceName":"1"}),"instanceName":"1"}),"instanceName":"1"}),"instanceName":"1"}),"instanceName":"1"}),"instanceName":"1"});
            var Q1601;
            Q1601=makeQuery(id+"F13.opPattern","COPY",BODY,{"derivedFrom":makeQuery(id+"F8.opPattern","COPY",BODY,{"derivedFrom":makeQuery(id+"F6.opPattern","COPY",BODY,{"derivedFrom":makeQuery(id+"F5.opPattern","COPY",BODY,{"derivedFrom":makeQuery(id+"F1.opRevolve","SWEPT_BODY",BODY,{"disambiguationData":[OSD([sQuery(id+"F0.wireOp",EDGE,"E1")])]}),"instanceName":"1"}),"instanceName":"1"}),"instanceName":"1"}),"instanceName":"1"});
            var Q1602;
            Q1602=makeQuery(id+"F13.opPattern","COPY",BODY,{"derivedFrom":makeQuery(id+"F8.opPattern","COPY",BODY,{"derivedFrom":makeQuery(id+"F6.opPattern","COPY",BODY,{"derivedFrom":makeQuery(id+"F5.opPattern","COPY",BODY,{"derivedFrom":makeQuery(id+"F2.opPattern","COPY",BODY,{"derivedFrom":makeQuery(id+"F1.opRevolve","SWEPT_BODY",BODY,{"disambiguationData":[OSD([sQuery(id+"F0.wireOp",EDGE,"E1")])]}),"instanceName":"1"}),"instanceName":"1"}),"instanceName":"1"}),"instanceName":"1"}),"instanceName":"1"});
            var Q1603;
            Q1603=makeQuery(id+"F13.opPattern","COPY",BODY,{"derivedFrom":makeQuery(id+"F8.opPattern","COPY",BODY,{"derivedFrom":makeQuery(id+"F6.opPattern","COPY",BODY,{"derivedFrom":makeQuery(id+"F5.opPattern","COPY",BODY,{"derivedFrom":makeQuery(id+"F3.opPattern","COPY",BODY,{"derivedFrom":makeQuery(id+"F2.opPattern","COPY",BODY,{"derivedFrom":makeQuery(id+"F1.opRevolve","SWEPT_BODY",BODY,{"disambiguationData":[OSD([sQuery(id+"F0.wireOp",EDGE,"E1")])]}),"instanceName":"1"}),"instanceName":"1"}),"instanceName":"1"}),"instanceName":"1"}),"instanceName":"1"}),"instanceName":"1"});
            var Q1604;
            Q1604=makeQuery(id+"F13.opPattern","COPY",BODY,{"derivedFrom":makeQuery(id+"F8.opPattern","COPY",BODY,{"derivedFrom":makeQuery(id+"F6.opPattern","COPY",BODY,{"derivedFrom":makeQuery(id+"F5.opPattern","COPY",BODY,{"derivedFrom":makeQuery(id+"F4.opPattern","COPY",BODY,{"derivedFrom":makeQuery(id+"F1.opRevolve","SWEPT_BODY",BODY,{"disambiguationData":[OSD([sQuery(id+"F0.wireOp",EDGE,"E1")])]}),"instanceName":"1"}),"instanceName":"1"}),"instanceName":"1"}),"instanceName":"1"}),"instanceName":"1"});
            var Q1605;
            Q1605=makeQuery(id+"F13.opPattern","COPY",BODY,{"derivedFrom":makeQuery(id+"F8.opPattern","COPY",BODY,{"derivedFrom":makeQuery(id+"F6.opPattern","COPY",BODY,{"derivedFrom":makeQuery(id+"F5.opPattern","COPY",BODY,{"derivedFrom":makeQuery(id+"F4.opPattern","COPY",BODY,{"derivedFrom":makeQuery(id+"F2.opPattern","COPY",BODY,{"derivedFrom":makeQuery(id+"F1.opRevolve","SWEPT_BODY",BODY,{"disambiguationData":[OSD([sQuery(id+"F0.wireOp",EDGE,"E1")])]}),"instanceName":"1"}),"instanceName":"1"}),"instanceName":"1"}),"instanceName":"1"}),"instanceName":"1"}),"instanceName":"1"});
            var Q1606;
            Q1606=makeQuery(id+"F13.opPattern","COPY",BODY,{"derivedFrom":makeQuery(id+"F8.opPattern","COPY",BODY,{"derivedFrom":makeQuery(id+"F6.opPattern","COPY",BODY,{"derivedFrom":makeQuery(id+"F5.opPattern","COPY",BODY,{"derivedFrom":makeQuery(id+"F4.opPattern","COPY",BODY,{"derivedFrom":makeQuery(id+"F3.opPattern","COPY",BODY,{"derivedFrom":makeQuery(id+"F2.opPattern","COPY",BODY,{"derivedFrom":makeQuery(id+"F1.opRevolve","SWEPT_BODY",BODY,{"disambiguationData":[OSD([sQuery(id+"F0.wireOp",EDGE,"E1")])]}),"instanceName":"1"}),"instanceName":"1"}),"instanceName":"1"}),"instanceName":"1"}),"instanceName":"1"}),"instanceName":"1"}),"instanceName":"1"});
            var Q1607;
            Q1607=makeQuery(id+"F13.opPattern","COPY",BODY,{"derivedFrom":makeQuery(id+"F8.opPattern","COPY",BODY,{"derivedFrom":makeQuery(id+"F7.opPattern","COPY",BODY,{"derivedFrom":makeQuery(id+"F1.opRevolve","SWEPT_BODY",BODY,{"disambiguationData":[OSD([sQuery(id+"F0.wireOp",EDGE,"E1")])]}),"instanceName":"1"}),"instanceName":"1"}),"instanceName":"1"});
            var Q1608;
            Q1608=makeQuery(id+"F13.opPattern","COPY",BODY,{"derivedFrom":makeQuery(id+"F8.opPattern","COPY",BODY,{"derivedFrom":makeQuery(id+"F7.opPattern","COPY",BODY,{"derivedFrom":makeQuery(id+"F2.opPattern","COPY",BODY,{"derivedFrom":makeQuery(id+"F1.opRevolve","SWEPT_BODY",BODY,{"disambiguationData":[OSD([sQuery(id+"F0.wireOp",EDGE,"E1")])]}),"instanceName":"1"}),"instanceName":"1"}),"instanceName":"1"}),"instanceName":"1"});
            var Q1609;
            Q1609=makeQuery(id+"F13.opPattern","COPY",BODY,{"derivedFrom":makeQuery(id+"F8.opPattern","COPY",BODY,{"derivedFrom":makeQuery(id+"F7.opPattern","COPY",BODY,{"derivedFrom":makeQuery(id+"F3.opPattern","COPY",BODY,{"derivedFrom":makeQuery(id+"F2.opPattern","COPY",BODY,{"derivedFrom":makeQuery(id+"F1.opRevolve","SWEPT_BODY",BODY,{"disambiguationData":[OSD([sQuery(id+"F0.wireOp",EDGE,"E1")])]}),"instanceName":"1"}),"instanceName":"1"}),"instanceName":"1"}),"instanceName":"1"}),"instanceName":"1"});
            var Q1610;
            Q1610=makeQuery(id+"F13.opPattern","COPY",BODY,{"derivedFrom":makeQuery(id+"F8.opPattern","COPY",BODY,{"derivedFrom":makeQuery(id+"F7.opPattern","COPY",BODY,{"derivedFrom":makeQuery(id+"F4.opPattern","COPY",BODY,{"derivedFrom":makeQuery(id+"F1.opRevolve","SWEPT_BODY",BODY,{"disambiguationData":[OSD([sQuery(id+"F0.wireOp",EDGE,"E1")])]}),"instanceName":"1"}),"instanceName":"1"}),"instanceName":"1"}),"instanceName":"1"});
            var Q1611;
            Q1611=makeQuery(id+"F13.opPattern","COPY",BODY,{"derivedFrom":makeQuery(id+"F8.opPattern","COPY",BODY,{"derivedFrom":makeQuery(id+"F7.opPattern","COPY",BODY,{"derivedFrom":makeQuery(id+"F4.opPattern","COPY",BODY,{"derivedFrom":makeQuery(id+"F2.opPattern","COPY",BODY,{"derivedFrom":makeQuery(id+"F1.opRevolve","SWEPT_BODY",BODY,{"disambiguationData":[OSD([sQuery(id+"F0.wireOp",EDGE,"E1")])]}),"instanceName":"1"}),"instanceName":"1"}),"instanceName":"1"}),"instanceName":"1"}),"instanceName":"1"});
            var Q1612;
            Q1612=makeQuery(id+"F13.opPattern","COPY",BODY,{"derivedFrom":makeQuery(id+"F8.opPattern","COPY",BODY,{"derivedFrom":makeQuery(id+"F7.opPattern","COPY",BODY,{"derivedFrom":makeQuery(id+"F4.opPattern","COPY",BODY,{"derivedFrom":makeQuery(id+"F3.opPattern","COPY",BODY,{"derivedFrom":makeQuery(id+"F2.opPattern","COPY",BODY,{"derivedFrom":makeQuery(id+"F1.opRevolve","SWEPT_BODY",BODY,{"disambiguationData":[OSD([sQuery(id+"F0.wireOp",EDGE,"E1")])]}),"instanceName":"1"}),"instanceName":"1"}),"instanceName":"1"}),"instanceName":"1"}),"instanceName":"1"}),"instanceName":"1"});
            var Q1613;
            Q1613=makeQuery(id+"F13.opPattern","COPY",BODY,{"derivedFrom":makeQuery(id+"F8.opPattern","COPY",BODY,{"derivedFrom":makeQuery(id+"F7.opPattern","COPY",BODY,{"derivedFrom":makeQuery(id+"F5.opPattern","COPY",BODY,{"derivedFrom":makeQuery(id+"F1.opRevolve","SWEPT_BODY",BODY,{"disambiguationData":[OSD([sQuery(id+"F0.wireOp",EDGE,"E1")])]}),"instanceName":"1"}),"instanceName":"1"}),"instanceName":"1"}),"instanceName":"1"});
            var Q1614;
            Q1614=makeQuery(id+"F13.opPattern","COPY",BODY,{"derivedFrom":makeQuery(id+"F8.opPattern","COPY",BODY,{"derivedFrom":makeQuery(id+"F7.opPattern","COPY",BODY,{"derivedFrom":makeQuery(id+"F5.opPattern","COPY",BODY,{"derivedFrom":makeQuery(id+"F2.opPattern","COPY",BODY,{"derivedFrom":makeQuery(id+"F1.opRevolve","SWEPT_BODY",BODY,{"disambiguationData":[OSD([sQuery(id+"F0.wireOp",EDGE,"E1")])]}),"instanceName":"1"}),"instanceName":"1"}),"instanceName":"1"}),"instanceName":"1"}),"instanceName":"1"});
            var Q1615;
            Q1615=makeQuery(id+"F13.opPattern","COPY",BODY,{"derivedFrom":makeQuery(id+"F8.opPattern","COPY",BODY,{"derivedFrom":makeQuery(id+"F7.opPattern","COPY",BODY,{"derivedFrom":makeQuery(id+"F5.opPattern","COPY",BODY,{"derivedFrom":makeQuery(id+"F3.opPattern","COPY",BODY,{"derivedFrom":makeQuery(id+"F2.opPattern","COPY",BODY,{"derivedFrom":makeQuery(id+"F1.opRevolve","SWEPT_BODY",BODY,{"disambiguationData":[OSD([sQuery(id+"F0.wireOp",EDGE,"E1")])]}),"instanceName":"1"}),"instanceName":"1"}),"instanceName":"1"}),"instanceName":"1"}),"instanceName":"1"}),"instanceName":"1"});
            var Q1616;
            Q1616=makeQuery(id+"F13.opPattern","COPY",BODY,{"derivedFrom":makeQuery(id+"F8.opPattern","COPY",BODY,{"derivedFrom":makeQuery(id+"F7.opPattern","COPY",BODY,{"derivedFrom":makeQuery(id+"F5.opPattern","COPY",BODY,{"derivedFrom":makeQuery(id+"F4.opPattern","COPY",BODY,{"derivedFrom":makeQuery(id+"F1.opRevolve","SWEPT_BODY",BODY,{"disambiguationData":[OSD([sQuery(id+"F0.wireOp",EDGE,"E1")])]}),"instanceName":"1"}),"instanceName":"1"}),"instanceName":"1"}),"instanceName":"1"}),"instanceName":"1"});
            var Q1617;
            Q1617=makeQuery(id+"F13.opPattern","COPY",BODY,{"derivedFrom":makeQuery(id+"F8.opPattern","COPY",BODY,{"derivedFrom":makeQuery(id+"F7.opPattern","COPY",BODY,{"derivedFrom":makeQuery(id+"F5.opPattern","COPY",BODY,{"derivedFrom":makeQuery(id+"F4.opPattern","COPY",BODY,{"derivedFrom":makeQuery(id+"F2.opPattern","COPY",BODY,{"derivedFrom":makeQuery(id+"F1.opRevolve","SWEPT_BODY",BODY,{"disambiguationData":[OSD([sQuery(id+"F0.wireOp",EDGE,"E1")])]}),"instanceName":"1"}),"instanceName":"1"}),"instanceName":"1"}),"instanceName":"1"}),"instanceName":"1"}),"instanceName":"1"});
            var Q1618;
            Q1618=makeQuery(id+"F13.opPattern","COPY",BODY,{"derivedFrom":makeQuery(id+"F8.opPattern","COPY",BODY,{"derivedFrom":makeQuery(id+"F7.opPattern","COPY",BODY,{"derivedFrom":makeQuery(id+"F5.opPattern","COPY",BODY,{"derivedFrom":makeQuery(id+"F4.opPattern","COPY",BODY,{"derivedFrom":makeQuery(id+"F3.opPattern","COPY",BODY,{"derivedFrom":makeQuery(id+"F2.opPattern","COPY",BODY,{"derivedFrom":makeQuery(id+"F1.opRevolve","SWEPT_BODY",BODY,{"disambiguationData":[OSD([sQuery(id+"F0.wireOp",EDGE,"E1")])]}),"instanceName":"1"}),"instanceName":"1"}),"instanceName":"1"}),"instanceName":"1"}),"instanceName":"1"}),"instanceName":"1"}),"instanceName":"1"});
            var Q1619;
            Q1619=makeQuery(id+"F13.opPattern","COPY",BODY,{"derivedFrom":makeQuery(id+"F8.opPattern","COPY",BODY,{"derivedFrom":makeQuery(id+"F7.opPattern","COPY",BODY,{"derivedFrom":makeQuery(id+"F6.opPattern","COPY",BODY,{"derivedFrom":makeQuery(id+"F1.opRevolve","SWEPT_BODY",BODY,{"disambiguationData":[OSD([sQuery(id+"F0.wireOp",EDGE,"E1")])]}),"instanceName":"1"}),"instanceName":"1"}),"instanceName":"1"}),"instanceName":"1"});
            var Q1620;
            Q1620=makeQuery(id+"F13.opPattern","COPY",BODY,{"derivedFrom":makeQuery(id+"F8.opPattern","COPY",BODY,{"derivedFrom":makeQuery(id+"F7.opPattern","COPY",BODY,{"derivedFrom":makeQuery(id+"F6.opPattern","COPY",BODY,{"derivedFrom":makeQuery(id+"F2.opPattern","COPY",BODY,{"derivedFrom":makeQuery(id+"F1.opRevolve","SWEPT_BODY",BODY,{"disambiguationData":[OSD([sQuery(id+"F0.wireOp",EDGE,"E1")])]}),"instanceName":"1"}),"instanceName":"1"}),"instanceName":"1"}),"instanceName":"1"}),"instanceName":"1"});
            var Q1621;
            Q1621=makeQuery(id+"F13.opPattern","COPY",BODY,{"derivedFrom":makeQuery(id+"F8.opPattern","COPY",BODY,{"derivedFrom":makeQuery(id+"F7.opPattern","COPY",BODY,{"derivedFrom":makeQuery(id+"F6.opPattern","COPY",BODY,{"derivedFrom":makeQuery(id+"F3.opPattern","COPY",BODY,{"derivedFrom":makeQuery(id+"F2.opPattern","COPY",BODY,{"derivedFrom":makeQuery(id+"F1.opRevolve","SWEPT_BODY",BODY,{"disambiguationData":[OSD([sQuery(id+"F0.wireOp",EDGE,"E1")])]}),"instanceName":"1"}),"instanceName":"1"}),"instanceName":"1"}),"instanceName":"1"}),"instanceName":"1"}),"instanceName":"1"});
            var Q1622;
            Q1622=makeQuery(id+"F13.opPattern","COPY",BODY,{"derivedFrom":makeQuery(id+"F8.opPattern","COPY",BODY,{"derivedFrom":makeQuery(id+"F7.opPattern","COPY",BODY,{"derivedFrom":makeQuery(id+"F6.opPattern","COPY",BODY,{"derivedFrom":makeQuery(id+"F4.opPattern","COPY",BODY,{"derivedFrom":makeQuery(id+"F1.opRevolve","SWEPT_BODY",BODY,{"disambiguationData":[OSD([sQuery(id+"F0.wireOp",EDGE,"E1")])]}),"instanceName":"1"}),"instanceName":"1"}),"instanceName":"1"}),"instanceName":"1"}),"instanceName":"1"});
            var Q1623;
            Q1623=makeQuery(id+"F13.opPattern","COPY",BODY,{"derivedFrom":makeQuery(id+"F8.opPattern","COPY",BODY,{"derivedFrom":makeQuery(id+"F7.opPattern","COPY",BODY,{"derivedFrom":makeQuery(id+"F6.opPattern","COPY",BODY,{"derivedFrom":makeQuery(id+"F4.opPattern","COPY",BODY,{"derivedFrom":makeQuery(id+"F2.opPattern","COPY",BODY,{"derivedFrom":makeQuery(id+"F1.opRevolve","SWEPT_BODY",BODY,{"disambiguationData":[OSD([sQuery(id+"F0.wireOp",EDGE,"E1")])]}),"instanceName":"1"}),"instanceName":"1"}),"instanceName":"1"}),"instanceName":"1"}),"instanceName":"1"}),"instanceName":"1"});
            var Q1624;
            Q1624=makeQuery(id+"F13.opPattern","COPY",BODY,{"derivedFrom":makeQuery(id+"F8.opPattern","COPY",BODY,{"derivedFrom":makeQuery(id+"F7.opPattern","COPY",BODY,{"derivedFrom":makeQuery(id+"F6.opPattern","COPY",BODY,{"derivedFrom":makeQuery(id+"F4.opPattern","COPY",BODY,{"derivedFrom":makeQuery(id+"F3.opPattern","COPY",BODY,{"derivedFrom":makeQuery(id+"F2.opPattern","COPY",BODY,{"derivedFrom":makeQuery(id+"F1.opRevolve","SWEPT_BODY",BODY,{"disambiguationData":[OSD([sQuery(id+"F0.wireOp",EDGE,"E1")])]}),"instanceName":"1"}),"instanceName":"1"}),"instanceName":"1"}),"instanceName":"1"}),"instanceName":"1"}),"instanceName":"1"}),"instanceName":"1"});
            var Q1625;
            Q1625=makeQuery(id+"F13.opPattern","COPY",BODY,{"derivedFrom":makeQuery(id+"F8.opPattern","COPY",BODY,{"derivedFrom":makeQuery(id+"F7.opPattern","COPY",BODY,{"derivedFrom":makeQuery(id+"F6.opPattern","COPY",BODY,{"derivedFrom":makeQuery(id+"F5.opPattern","COPY",BODY,{"derivedFrom":makeQuery(id+"F1.opRevolve","SWEPT_BODY",BODY,{"disambiguationData":[OSD([sQuery(id+"F0.wireOp",EDGE,"E1")])]}),"instanceName":"1"}),"instanceName":"1"}),"instanceName":"1"}),"instanceName":"1"}),"instanceName":"1"});
            var Q1626;
            Q1626=makeQuery(id+"F13.opPattern","COPY",BODY,{"derivedFrom":makeQuery(id+"F8.opPattern","COPY",BODY,{"derivedFrom":makeQuery(id+"F7.opPattern","COPY",BODY,{"derivedFrom":makeQuery(id+"F6.opPattern","COPY",BODY,{"derivedFrom":makeQuery(id+"F5.opPattern","COPY",BODY,{"derivedFrom":makeQuery(id+"F2.opPattern","COPY",BODY,{"derivedFrom":makeQuery(id+"F1.opRevolve","SWEPT_BODY",BODY,{"disambiguationData":[OSD([sQuery(id+"F0.wireOp",EDGE,"E1")])]}),"instanceName":"1"}),"instanceName":"1"}),"instanceName":"1"}),"instanceName":"1"}),"instanceName":"1"}),"instanceName":"1"});
            var Q1627;
            Q1627=makeQuery(id+"F13.opPattern","COPY",BODY,{"derivedFrom":makeQuery(id+"F8.opPattern","COPY",BODY,{"derivedFrom":makeQuery(id+"F7.opPattern","COPY",BODY,{"derivedFrom":makeQuery(id+"F6.opPattern","COPY",BODY,{"derivedFrom":makeQuery(id+"F5.opPattern","COPY",BODY,{"derivedFrom":makeQuery(id+"F3.opPattern","COPY",BODY,{"derivedFrom":makeQuery(id+"F2.opPattern","COPY",BODY,{"derivedFrom":makeQuery(id+"F1.opRevolve","SWEPT_BODY",BODY,{"disambiguationData":[OSD([sQuery(id+"F0.wireOp",EDGE,"E1")])]}),"instanceName":"1"}),"instanceName":"1"}),"instanceName":"1"}),"instanceName":"1"}),"instanceName":"1"}),"instanceName":"1"}),"instanceName":"1"});
            var Q1628;
            Q1628=makeQuery(id+"F13.opPattern","COPY",BODY,{"derivedFrom":makeQuery(id+"F8.opPattern","COPY",BODY,{"derivedFrom":makeQuery(id+"F7.opPattern","COPY",BODY,{"derivedFrom":makeQuery(id+"F6.opPattern","COPY",BODY,{"derivedFrom":makeQuery(id+"F5.opPattern","COPY",BODY,{"derivedFrom":makeQuery(id+"F4.opPattern","COPY",BODY,{"derivedFrom":makeQuery(id+"F1.opRevolve","SWEPT_BODY",BODY,{"disambiguationData":[OSD([sQuery(id+"F0.wireOp",EDGE,"E1")])]}),"instanceName":"1"}),"instanceName":"1"}),"instanceName":"1"}),"instanceName":"1"}),"instanceName":"1"}),"instanceName":"1"});
            var Q1629;
            Q1629=makeQuery(id+"F13.opPattern","COPY",BODY,{"derivedFrom":makeQuery(id+"F8.opPattern","COPY",BODY,{"derivedFrom":makeQuery(id+"F7.opPattern","COPY",BODY,{"derivedFrom":makeQuery(id+"F6.opPattern","COPY",BODY,{"derivedFrom":makeQuery(id+"F5.opPattern","COPY",BODY,{"derivedFrom":makeQuery(id+"F4.opPattern","COPY",BODY,{"derivedFrom":makeQuery(id+"F2.opPattern","COPY",BODY,{"derivedFrom":makeQuery(id+"F1.opRevolve","SWEPT_BODY",BODY,{"disambiguationData":[OSD([sQuery(id+"F0.wireOp",EDGE,"E1")])]}),"instanceName":"1"}),"instanceName":"1"}),"instanceName":"1"}),"instanceName":"1"}),"instanceName":"1"}),"instanceName":"1"}),"instanceName":"1"});
            var Q1630;
            Q1630=makeQuery(id+"F13.opPattern","COPY",BODY,{"derivedFrom":makeQuery(id+"F8.opPattern","COPY",BODY,{"derivedFrom":makeQuery(id+"F7.opPattern","COPY",BODY,{"derivedFrom":makeQuery(id+"F6.opPattern","COPY",BODY,{"derivedFrom":makeQuery(id+"F5.opPattern","COPY",BODY,{"derivedFrom":makeQuery(id+"F4.opPattern","COPY",BODY,{"derivedFrom":makeQuery(id+"F3.opPattern","COPY",BODY,{"derivedFrom":makeQuery(id+"F2.opPattern","COPY",BODY,{"derivedFrom":makeQuery(id+"F1.opRevolve","SWEPT_BODY",BODY,{"disambiguationData":[OSD([sQuery(id+"F0.wireOp",EDGE,"E1")])]}),"instanceName":"1"}),"instanceName":"1"}),"instanceName":"1"}),"instanceName":"1"}),"instanceName":"1"}),"instanceName":"1"}),"instanceName":"1"}),"instanceName":"1"});
            var Q1631;
            Q1631=makeQuery(id+"F13.opPattern","COPY",BODY,{"derivedFrom":makeQuery(id+"F9.opPattern","COPY",BODY,{"derivedFrom":makeQuery(id+"F1.opRevolve","SWEPT_BODY",BODY,{"disambiguationData":[OSD([sQuery(id+"F0.wireOp",EDGE,"E1")])]}),"instanceName":"1"}),"instanceName":"1"});
            var Q1632;
            Q1632=makeQuery(id+"F13.opPattern","COPY",BODY,{"derivedFrom":makeQuery(id+"F9.opPattern","COPY",BODY,{"derivedFrom":makeQuery(id+"F2.opPattern","COPY",BODY,{"derivedFrom":makeQuery(id+"F1.opRevolve","SWEPT_BODY",BODY,{"disambiguationData":[OSD([sQuery(id+"F0.wireOp",EDGE,"E1")])]}),"instanceName":"1"}),"instanceName":"1"}),"instanceName":"1"});
            var Q1633;
            Q1633=makeQuery(id+"F13.opPattern","COPY",BODY,{"derivedFrom":makeQuery(id+"F9.opPattern","COPY",BODY,{"derivedFrom":makeQuery(id+"F3.opPattern","COPY",BODY,{"derivedFrom":makeQuery(id+"F2.opPattern","COPY",BODY,{"derivedFrom":makeQuery(id+"F1.opRevolve","SWEPT_BODY",BODY,{"disambiguationData":[OSD([sQuery(id+"F0.wireOp",EDGE,"E1")])]}),"instanceName":"1"}),"instanceName":"1"}),"instanceName":"1"}),"instanceName":"1"});
            var Q1634;
            Q1634=makeQuery(id+"F13.opPattern","COPY",BODY,{"derivedFrom":makeQuery(id+"F9.opPattern","COPY",BODY,{"derivedFrom":makeQuery(id+"F4.opPattern","COPY",BODY,{"derivedFrom":makeQuery(id+"F1.opRevolve","SWEPT_BODY",BODY,{"disambiguationData":[OSD([sQuery(id+"F0.wireOp",EDGE,"E1")])]}),"instanceName":"1"}),"instanceName":"1"}),"instanceName":"1"});
            var Q1635;
            Q1635=makeQuery(id+"F13.opPattern","COPY",BODY,{"derivedFrom":makeQuery(id+"F9.opPattern","COPY",BODY,{"derivedFrom":makeQuery(id+"F4.opPattern","COPY",BODY,{"derivedFrom":makeQuery(id+"F2.opPattern","COPY",BODY,{"derivedFrom":makeQuery(id+"F1.opRevolve","SWEPT_BODY",BODY,{"disambiguationData":[OSD([sQuery(id+"F0.wireOp",EDGE,"E1")])]}),"instanceName":"1"}),"instanceName":"1"}),"instanceName":"1"}),"instanceName":"1"});
            var Q1636;
            Q1636=makeQuery(id+"F13.opPattern","COPY",BODY,{"derivedFrom":makeQuery(id+"F9.opPattern","COPY",BODY,{"derivedFrom":makeQuery(id+"F4.opPattern","COPY",BODY,{"derivedFrom":makeQuery(id+"F3.opPattern","COPY",BODY,{"derivedFrom":makeQuery(id+"F2.opPattern","COPY",BODY,{"derivedFrom":makeQuery(id+"F1.opRevolve","SWEPT_BODY",BODY,{"disambiguationData":[OSD([sQuery(id+"F0.wireOp",EDGE,"E1")])]}),"instanceName":"1"}),"instanceName":"1"}),"instanceName":"1"}),"instanceName":"1"}),"instanceName":"1"});
            var Q1637;
            Q1637=makeQuery(id+"F13.opPattern","COPY",BODY,{"derivedFrom":makeQuery(id+"F9.opPattern","COPY",BODY,{"derivedFrom":makeQuery(id+"F5.opPattern","COPY",BODY,{"derivedFrom":makeQuery(id+"F1.opRevolve","SWEPT_BODY",BODY,{"disambiguationData":[OSD([sQuery(id+"F0.wireOp",EDGE,"E1")])]}),"instanceName":"1"}),"instanceName":"1"}),"instanceName":"1"});
            var Q1638;
            Q1638=makeQuery(id+"F13.opPattern","COPY",BODY,{"derivedFrom":makeQuery(id+"F9.opPattern","COPY",BODY,{"derivedFrom":makeQuery(id+"F5.opPattern","COPY",BODY,{"derivedFrom":makeQuery(id+"F2.opPattern","COPY",BODY,{"derivedFrom":makeQuery(id+"F1.opRevolve","SWEPT_BODY",BODY,{"disambiguationData":[OSD([sQuery(id+"F0.wireOp",EDGE,"E1")])]}),"instanceName":"1"}),"instanceName":"1"}),"instanceName":"1"}),"instanceName":"1"});
            var Q1639;
            Q1639=makeQuery(id+"F13.opPattern","COPY",BODY,{"derivedFrom":makeQuery(id+"F9.opPattern","COPY",BODY,{"derivedFrom":makeQuery(id+"F5.opPattern","COPY",BODY,{"derivedFrom":makeQuery(id+"F3.opPattern","COPY",BODY,{"derivedFrom":makeQuery(id+"F2.opPattern","COPY",BODY,{"derivedFrom":makeQuery(id+"F1.opRevolve","SWEPT_BODY",BODY,{"disambiguationData":[OSD([sQuery(id+"F0.wireOp",EDGE,"E1")])]}),"instanceName":"1"}),"instanceName":"1"}),"instanceName":"1"}),"instanceName":"1"}),"instanceName":"1"});
            var Q1640;
            Q1640=makeQuery(id+"F13.opPattern","COPY",BODY,{"derivedFrom":makeQuery(id+"F9.opPattern","COPY",BODY,{"derivedFrom":makeQuery(id+"F5.opPattern","COPY",BODY,{"derivedFrom":makeQuery(id+"F4.opPattern","COPY",BODY,{"derivedFrom":makeQuery(id+"F1.opRevolve","SWEPT_BODY",BODY,{"disambiguationData":[OSD([sQuery(id+"F0.wireOp",EDGE,"E1")])]}),"instanceName":"1"}),"instanceName":"1"}),"instanceName":"1"}),"instanceName":"1"});
            var Q1641;
            Q1641=makeQuery(id+"F13.opPattern","COPY",BODY,{"derivedFrom":makeQuery(id+"F9.opPattern","COPY",BODY,{"derivedFrom":makeQuery(id+"F5.opPattern","COPY",BODY,{"derivedFrom":makeQuery(id+"F4.opPattern","COPY",BODY,{"derivedFrom":makeQuery(id+"F2.opPattern","COPY",BODY,{"derivedFrom":makeQuery(id+"F1.opRevolve","SWEPT_BODY",BODY,{"disambiguationData":[OSD([sQuery(id+"F0.wireOp",EDGE,"E1")])]}),"instanceName":"1"}),"instanceName":"1"}),"instanceName":"1"}),"instanceName":"1"}),"instanceName":"1"});
            var Q1642;
            Q1642=makeQuery(id+"F13.opPattern","COPY",BODY,{"derivedFrom":makeQuery(id+"F9.opPattern","COPY",BODY,{"derivedFrom":makeQuery(id+"F5.opPattern","COPY",BODY,{"derivedFrom":makeQuery(id+"F4.opPattern","COPY",BODY,{"derivedFrom":makeQuery(id+"F3.opPattern","COPY",BODY,{"derivedFrom":makeQuery(id+"F2.opPattern","COPY",BODY,{"derivedFrom":makeQuery(id+"F1.opRevolve","SWEPT_BODY",BODY,{"disambiguationData":[OSD([sQuery(id+"F0.wireOp",EDGE,"E1")])]}),"instanceName":"1"}),"instanceName":"1"}),"instanceName":"1"}),"instanceName":"1"}),"instanceName":"1"}),"instanceName":"1"});
            var Q1643;
            Q1643=makeQuery(id+"F13.opPattern","COPY",BODY,{"derivedFrom":makeQuery(id+"F9.opPattern","COPY",BODY,{"derivedFrom":makeQuery(id+"F6.opPattern","COPY",BODY,{"derivedFrom":makeQuery(id+"F1.opRevolve","SWEPT_BODY",BODY,{"disambiguationData":[OSD([sQuery(id+"F0.wireOp",EDGE,"E1")])]}),"instanceName":"1"}),"instanceName":"1"}),"instanceName":"1"});
            var Q1644;
            Q1644=makeQuery(id+"F13.opPattern","COPY",BODY,{"derivedFrom":makeQuery(id+"F9.opPattern","COPY",BODY,{"derivedFrom":makeQuery(id+"F6.opPattern","COPY",BODY,{"derivedFrom":makeQuery(id+"F2.opPattern","COPY",BODY,{"derivedFrom":makeQuery(id+"F1.opRevolve","SWEPT_BODY",BODY,{"disambiguationData":[OSD([sQuery(id+"F0.wireOp",EDGE,"E1")])]}),"instanceName":"1"}),"instanceName":"1"}),"instanceName":"1"}),"instanceName":"1"});
            var Q1645;
            Q1645=makeQuery(id+"F13.opPattern","COPY",BODY,{"derivedFrom":makeQuery(id+"F9.opPattern","COPY",BODY,{"derivedFrom":makeQuery(id+"F6.opPattern","COPY",BODY,{"derivedFrom":makeQuery(id+"F3.opPattern","COPY",BODY,{"derivedFrom":makeQuery(id+"F2.opPattern","COPY",BODY,{"derivedFrom":makeQuery(id+"F1.opRevolve","SWEPT_BODY",BODY,{"disambiguationData":[OSD([sQuery(id+"F0.wireOp",EDGE,"E1")])]}),"instanceName":"1"}),"instanceName":"1"}),"instanceName":"1"}),"instanceName":"1"}),"instanceName":"1"});
            var Q1646;
            Q1646=makeQuery(id+"F13.opPattern","COPY",BODY,{"derivedFrom":makeQuery(id+"F9.opPattern","COPY",BODY,{"derivedFrom":makeQuery(id+"F6.opPattern","COPY",BODY,{"derivedFrom":makeQuery(id+"F4.opPattern","COPY",BODY,{"derivedFrom":makeQuery(id+"F1.opRevolve","SWEPT_BODY",BODY,{"disambiguationData":[OSD([sQuery(id+"F0.wireOp",EDGE,"E1")])]}),"instanceName":"1"}),"instanceName":"1"}),"instanceName":"1"}),"instanceName":"1"});
            var Q1647;
            Q1647=makeQuery(id+"F13.opPattern","COPY",BODY,{"derivedFrom":makeQuery(id+"F9.opPattern","COPY",BODY,{"derivedFrom":makeQuery(id+"F6.opPattern","COPY",BODY,{"derivedFrom":makeQuery(id+"F4.opPattern","COPY",BODY,{"derivedFrom":makeQuery(id+"F2.opPattern","COPY",BODY,{"derivedFrom":makeQuery(id+"F1.opRevolve","SWEPT_BODY",BODY,{"disambiguationData":[OSD([sQuery(id+"F0.wireOp",EDGE,"E1")])]}),"instanceName":"1"}),"instanceName":"1"}),"instanceName":"1"}),"instanceName":"1"}),"instanceName":"1"});
            var Q1648;
            Q1648=makeQuery(id+"F13.opPattern","COPY",BODY,{"derivedFrom":makeQuery(id+"F9.opPattern","COPY",BODY,{"derivedFrom":makeQuery(id+"F6.opPattern","COPY",BODY,{"derivedFrom":makeQuery(id+"F4.opPattern","COPY",BODY,{"derivedFrom":makeQuery(id+"F3.opPattern","COPY",BODY,{"derivedFrom":makeQuery(id+"F2.opPattern","COPY",BODY,{"derivedFrom":makeQuery(id+"F1.opRevolve","SWEPT_BODY",BODY,{"disambiguationData":[OSD([sQuery(id+"F0.wireOp",EDGE,"E1")])]}),"instanceName":"1"}),"instanceName":"1"}),"instanceName":"1"}),"instanceName":"1"}),"instanceName":"1"}),"instanceName":"1"});
            var Q1649;
            Q1649=makeQuery(id+"F13.opPattern","COPY",BODY,{"derivedFrom":makeQuery(id+"F9.opPattern","COPY",BODY,{"derivedFrom":makeQuery(id+"F6.opPattern","COPY",BODY,{"derivedFrom":makeQuery(id+"F5.opPattern","COPY",BODY,{"derivedFrom":makeQuery(id+"F1.opRevolve","SWEPT_BODY",BODY,{"disambiguationData":[OSD([sQuery(id+"F0.wireOp",EDGE,"E1")])]}),"instanceName":"1"}),"instanceName":"1"}),"instanceName":"1"}),"instanceName":"1"});
            var Q1650;
            Q1650=makeQuery(id+"F13.opPattern","COPY",BODY,{"derivedFrom":makeQuery(id+"F9.opPattern","COPY",BODY,{"derivedFrom":makeQuery(id+"F6.opPattern","COPY",BODY,{"derivedFrom":makeQuery(id+"F5.opPattern","COPY",BODY,{"derivedFrom":makeQuery(id+"F2.opPattern","COPY",BODY,{"derivedFrom":makeQuery(id+"F1.opRevolve","SWEPT_BODY",BODY,{"disambiguationData":[OSD([sQuery(id+"F0.wireOp",EDGE,"E1")])]}),"instanceName":"1"}),"instanceName":"1"}),"instanceName":"1"}),"instanceName":"1"}),"instanceName":"1"});
            var Q1651;
            Q1651=makeQuery(id+"F13.opPattern","COPY",BODY,{"derivedFrom":makeQuery(id+"F9.opPattern","COPY",BODY,{"derivedFrom":makeQuery(id+"F6.opPattern","COPY",BODY,{"derivedFrom":makeQuery(id+"F5.opPattern","COPY",BODY,{"derivedFrom":makeQuery(id+"F3.opPattern","COPY",BODY,{"derivedFrom":makeQuery(id+"F2.opPattern","COPY",BODY,{"derivedFrom":makeQuery(id+"F1.opRevolve","SWEPT_BODY",BODY,{"disambiguationData":[OSD([sQuery(id+"F0.wireOp",EDGE,"E1")])]}),"instanceName":"1"}),"instanceName":"1"}),"instanceName":"1"}),"instanceName":"1"}),"instanceName":"1"}),"instanceName":"1"});
            var Q1652;
            Q1652=makeQuery(id+"F13.opPattern","COPY",BODY,{"derivedFrom":makeQuery(id+"F9.opPattern","COPY",BODY,{"derivedFrom":makeQuery(id+"F6.opPattern","COPY",BODY,{"derivedFrom":makeQuery(id+"F5.opPattern","COPY",BODY,{"derivedFrom":makeQuery(id+"F4.opPattern","COPY",BODY,{"derivedFrom":makeQuery(id+"F1.opRevolve","SWEPT_BODY",BODY,{"disambiguationData":[OSD([sQuery(id+"F0.wireOp",EDGE,"E1")])]}),"instanceName":"1"}),"instanceName":"1"}),"instanceName":"1"}),"instanceName":"1"}),"instanceName":"1"});
            var Q1653;
            Q1653=makeQuery(id+"F13.opPattern","COPY",BODY,{"derivedFrom":makeQuery(id+"F9.opPattern","COPY",BODY,{"derivedFrom":makeQuery(id+"F6.opPattern","COPY",BODY,{"derivedFrom":makeQuery(id+"F5.opPattern","COPY",BODY,{"derivedFrom":makeQuery(id+"F4.opPattern","COPY",BODY,{"derivedFrom":makeQuery(id+"F2.opPattern","COPY",BODY,{"derivedFrom":makeQuery(id+"F1.opRevolve","SWEPT_BODY",BODY,{"disambiguationData":[OSD([sQuery(id+"F0.wireOp",EDGE,"E1")])]}),"instanceName":"1"}),"instanceName":"1"}),"instanceName":"1"}),"instanceName":"1"}),"instanceName":"1"}),"instanceName":"1"});
            var Q1654;
            Q1654=makeQuery(id+"F13.opPattern","COPY",BODY,{"derivedFrom":makeQuery(id+"F9.opPattern","COPY",BODY,{"derivedFrom":makeQuery(id+"F6.opPattern","COPY",BODY,{"derivedFrom":makeQuery(id+"F5.opPattern","COPY",BODY,{"derivedFrom":makeQuery(id+"F4.opPattern","COPY",BODY,{"derivedFrom":makeQuery(id+"F3.opPattern","COPY",BODY,{"derivedFrom":makeQuery(id+"F2.opPattern","COPY",BODY,{"derivedFrom":makeQuery(id+"F1.opRevolve","SWEPT_BODY",BODY,{"disambiguationData":[OSD([sQuery(id+"F0.wireOp",EDGE,"E1")])]}),"instanceName":"1"}),"instanceName":"1"}),"instanceName":"1"}),"instanceName":"1"}),"instanceName":"1"}),"instanceName":"1"}),"instanceName":"1"});
            var Q1655;
            Q1655=makeQuery(id+"F13.opPattern","COPY",BODY,{"derivedFrom":makeQuery(id+"F9.opPattern","COPY",BODY,{"derivedFrom":makeQuery(id+"F7.opPattern","COPY",BODY,{"derivedFrom":makeQuery(id+"F1.opRevolve","SWEPT_BODY",BODY,{"disambiguationData":[OSD([sQuery(id+"F0.wireOp",EDGE,"E1")])]}),"instanceName":"1"}),"instanceName":"1"}),"instanceName":"1"});
            var Q1656;
            Q1656=makeQuery(id+"F13.opPattern","COPY",BODY,{"derivedFrom":makeQuery(id+"F9.opPattern","COPY",BODY,{"derivedFrom":makeQuery(id+"F7.opPattern","COPY",BODY,{"derivedFrom":makeQuery(id+"F2.opPattern","COPY",BODY,{"derivedFrom":makeQuery(id+"F1.opRevolve","SWEPT_BODY",BODY,{"disambiguationData":[OSD([sQuery(id+"F0.wireOp",EDGE,"E1")])]}),"instanceName":"1"}),"instanceName":"1"}),"instanceName":"1"}),"instanceName":"1"});
            var Q1657;
            Q1657=makeQuery(id+"F13.opPattern","COPY",BODY,{"derivedFrom":makeQuery(id+"F9.opPattern","COPY",BODY,{"derivedFrom":makeQuery(id+"F7.opPattern","COPY",BODY,{"derivedFrom":makeQuery(id+"F3.opPattern","COPY",BODY,{"derivedFrom":makeQuery(id+"F2.opPattern","COPY",BODY,{"derivedFrom":makeQuery(id+"F1.opRevolve","SWEPT_BODY",BODY,{"disambiguationData":[OSD([sQuery(id+"F0.wireOp",EDGE,"E1")])]}),"instanceName":"1"}),"instanceName":"1"}),"instanceName":"1"}),"instanceName":"1"}),"instanceName":"1"});
            var Q1658;
            Q1658=makeQuery(id+"F13.opPattern","COPY",BODY,{"derivedFrom":makeQuery(id+"F9.opPattern","COPY",BODY,{"derivedFrom":makeQuery(id+"F7.opPattern","COPY",BODY,{"derivedFrom":makeQuery(id+"F4.opPattern","COPY",BODY,{"derivedFrom":makeQuery(id+"F1.opRevolve","SWEPT_BODY",BODY,{"disambiguationData":[OSD([sQuery(id+"F0.wireOp",EDGE,"E1")])]}),"instanceName":"1"}),"instanceName":"1"}),"instanceName":"1"}),"instanceName":"1"});
            var Q1659;
            Q1659=makeQuery(id+"F13.opPattern","COPY",BODY,{"derivedFrom":makeQuery(id+"F9.opPattern","COPY",BODY,{"derivedFrom":makeQuery(id+"F7.opPattern","COPY",BODY,{"derivedFrom":makeQuery(id+"F4.opPattern","COPY",BODY,{"derivedFrom":makeQuery(id+"F2.opPattern","COPY",BODY,{"derivedFrom":makeQuery(id+"F1.opRevolve","SWEPT_BODY",BODY,{"disambiguationData":[OSD([sQuery(id+"F0.wireOp",EDGE,"E1")])]}),"instanceName":"1"}),"instanceName":"1"}),"instanceName":"1"}),"instanceName":"1"}),"instanceName":"1"});
            var Q1660;
            Q1660=makeQuery(id+"F13.opPattern","COPY",BODY,{"derivedFrom":makeQuery(id+"F9.opPattern","COPY",BODY,{"derivedFrom":makeQuery(id+"F7.opPattern","COPY",BODY,{"derivedFrom":makeQuery(id+"F4.opPattern","COPY",BODY,{"derivedFrom":makeQuery(id+"F3.opPattern","COPY",BODY,{"derivedFrom":makeQuery(id+"F2.opPattern","COPY",BODY,{"derivedFrom":makeQuery(id+"F1.opRevolve","SWEPT_BODY",BODY,{"disambiguationData":[OSD([sQuery(id+"F0.wireOp",EDGE,"E1")])]}),"instanceName":"1"}),"instanceName":"1"}),"instanceName":"1"}),"instanceName":"1"}),"instanceName":"1"}),"instanceName":"1"});
            var Q1661;
            Q1661=makeQuery(id+"F13.opPattern","COPY",BODY,{"derivedFrom":makeQuery(id+"F9.opPattern","COPY",BODY,{"derivedFrom":makeQuery(id+"F7.opPattern","COPY",BODY,{"derivedFrom":makeQuery(id+"F5.opPattern","COPY",BODY,{"derivedFrom":makeQuery(id+"F1.opRevolve","SWEPT_BODY",BODY,{"disambiguationData":[OSD([sQuery(id+"F0.wireOp",EDGE,"E1")])]}),"instanceName":"1"}),"instanceName":"1"}),"instanceName":"1"}),"instanceName":"1"});
            var Q1662;
            Q1662=makeQuery(id+"F13.opPattern","COPY",BODY,{"derivedFrom":makeQuery(id+"F9.opPattern","COPY",BODY,{"derivedFrom":makeQuery(id+"F7.opPattern","COPY",BODY,{"derivedFrom":makeQuery(id+"F5.opPattern","COPY",BODY,{"derivedFrom":makeQuery(id+"F2.opPattern","COPY",BODY,{"derivedFrom":makeQuery(id+"F1.opRevolve","SWEPT_BODY",BODY,{"disambiguationData":[OSD([sQuery(id+"F0.wireOp",EDGE,"E1")])]}),"instanceName":"1"}),"instanceName":"1"}),"instanceName":"1"}),"instanceName":"1"}),"instanceName":"1"});
            var Q1663;
            Q1663=makeQuery(id+"F13.opPattern","COPY",BODY,{"derivedFrom":makeQuery(id+"F9.opPattern","COPY",BODY,{"derivedFrom":makeQuery(id+"F7.opPattern","COPY",BODY,{"derivedFrom":makeQuery(id+"F5.opPattern","COPY",BODY,{"derivedFrom":makeQuery(id+"F3.opPattern","COPY",BODY,{"derivedFrom":makeQuery(id+"F2.opPattern","COPY",BODY,{"derivedFrom":makeQuery(id+"F1.opRevolve","SWEPT_BODY",BODY,{"disambiguationData":[OSD([sQuery(id+"F0.wireOp",EDGE,"E1")])]}),"instanceName":"1"}),"instanceName":"1"}),"instanceName":"1"}),"instanceName":"1"}),"instanceName":"1"}),"instanceName":"1"});
            var Q1664;
            Q1664=makeQuery(id+"F13.opPattern","COPY",BODY,{"derivedFrom":makeQuery(id+"F9.opPattern","COPY",BODY,{"derivedFrom":makeQuery(id+"F7.opPattern","COPY",BODY,{"derivedFrom":makeQuery(id+"F5.opPattern","COPY",BODY,{"derivedFrom":makeQuery(id+"F4.opPattern","COPY",BODY,{"derivedFrom":makeQuery(id+"F1.opRevolve","SWEPT_BODY",BODY,{"disambiguationData":[OSD([sQuery(id+"F0.wireOp",EDGE,"E1")])]}),"instanceName":"1"}),"instanceName":"1"}),"instanceName":"1"}),"instanceName":"1"}),"instanceName":"1"});
            var Q1665;
            Q1665=makeQuery(id+"F13.opPattern","COPY",BODY,{"derivedFrom":makeQuery(id+"F9.opPattern","COPY",BODY,{"derivedFrom":makeQuery(id+"F7.opPattern","COPY",BODY,{"derivedFrom":makeQuery(id+"F5.opPattern","COPY",BODY,{"derivedFrom":makeQuery(id+"F4.opPattern","COPY",BODY,{"derivedFrom":makeQuery(id+"F2.opPattern","COPY",BODY,{"derivedFrom":makeQuery(id+"F1.opRevolve","SWEPT_BODY",BODY,{"disambiguationData":[OSD([sQuery(id+"F0.wireOp",EDGE,"E1")])]}),"instanceName":"1"}),"instanceName":"1"}),"instanceName":"1"}),"instanceName":"1"}),"instanceName":"1"}),"instanceName":"1"});
            var Q1666;
            Q1666=makeQuery(id+"F13.opPattern","COPY",BODY,{"derivedFrom":makeQuery(id+"F9.opPattern","COPY",BODY,{"derivedFrom":makeQuery(id+"F7.opPattern","COPY",BODY,{"derivedFrom":makeQuery(id+"F5.opPattern","COPY",BODY,{"derivedFrom":makeQuery(id+"F4.opPattern","COPY",BODY,{"derivedFrom":makeQuery(id+"F3.opPattern","COPY",BODY,{"derivedFrom":makeQuery(id+"F2.opPattern","COPY",BODY,{"derivedFrom":makeQuery(id+"F1.opRevolve","SWEPT_BODY",BODY,{"disambiguationData":[OSD([sQuery(id+"F0.wireOp",EDGE,"E1")])]}),"instanceName":"1"}),"instanceName":"1"}),"instanceName":"1"}),"instanceName":"1"}),"instanceName":"1"}),"instanceName":"1"}),"instanceName":"1"});
            var Q1667;
            Q1667=makeQuery(id+"F13.opPattern","COPY",BODY,{"derivedFrom":makeQuery(id+"F9.opPattern","COPY",BODY,{"derivedFrom":makeQuery(id+"F7.opPattern","COPY",BODY,{"derivedFrom":makeQuery(id+"F6.opPattern","COPY",BODY,{"derivedFrom":makeQuery(id+"F1.opRevolve","SWEPT_BODY",BODY,{"disambiguationData":[OSD([sQuery(id+"F0.wireOp",EDGE,"E1")])]}),"instanceName":"1"}),"instanceName":"1"}),"instanceName":"1"}),"instanceName":"1"});
            var Q1668;
            Q1668=makeQuery(id+"F13.opPattern","COPY",BODY,{"derivedFrom":makeQuery(id+"F9.opPattern","COPY",BODY,{"derivedFrom":makeQuery(id+"F7.opPattern","COPY",BODY,{"derivedFrom":makeQuery(id+"F6.opPattern","COPY",BODY,{"derivedFrom":makeQuery(id+"F2.opPattern","COPY",BODY,{"derivedFrom":makeQuery(id+"F1.opRevolve","SWEPT_BODY",BODY,{"disambiguationData":[OSD([sQuery(id+"F0.wireOp",EDGE,"E1")])]}),"instanceName":"1"}),"instanceName":"1"}),"instanceName":"1"}),"instanceName":"1"}),"instanceName":"1"});
            var Q1669;
            Q1669=makeQuery(id+"F13.opPattern","COPY",BODY,{"derivedFrom":makeQuery(id+"F9.opPattern","COPY",BODY,{"derivedFrom":makeQuery(id+"F7.opPattern","COPY",BODY,{"derivedFrom":makeQuery(id+"F6.opPattern","COPY",BODY,{"derivedFrom":makeQuery(id+"F3.opPattern","COPY",BODY,{"derivedFrom":makeQuery(id+"F2.opPattern","COPY",BODY,{"derivedFrom":makeQuery(id+"F1.opRevolve","SWEPT_BODY",BODY,{"disambiguationData":[OSD([sQuery(id+"F0.wireOp",EDGE,"E1")])]}),"instanceName":"1"}),"instanceName":"1"}),"instanceName":"1"}),"instanceName":"1"}),"instanceName":"1"}),"instanceName":"1"});
            var Q1670;
            Q1670=makeQuery(id+"F13.opPattern","COPY",BODY,{"derivedFrom":makeQuery(id+"F9.opPattern","COPY",BODY,{"derivedFrom":makeQuery(id+"F7.opPattern","COPY",BODY,{"derivedFrom":makeQuery(id+"F6.opPattern","COPY",BODY,{"derivedFrom":makeQuery(id+"F4.opPattern","COPY",BODY,{"derivedFrom":makeQuery(id+"F1.opRevolve","SWEPT_BODY",BODY,{"disambiguationData":[OSD([sQuery(id+"F0.wireOp",EDGE,"E1")])]}),"instanceName":"1"}),"instanceName":"1"}),"instanceName":"1"}),"instanceName":"1"}),"instanceName":"1"});
            var Q1671;
            Q1671=makeQuery(id+"F13.opPattern","COPY",BODY,{"derivedFrom":makeQuery(id+"F9.opPattern","COPY",BODY,{"derivedFrom":makeQuery(id+"F7.opPattern","COPY",BODY,{"derivedFrom":makeQuery(id+"F6.opPattern","COPY",BODY,{"derivedFrom":makeQuery(id+"F4.opPattern","COPY",BODY,{"derivedFrom":makeQuery(id+"F2.opPattern","COPY",BODY,{"derivedFrom":makeQuery(id+"F1.opRevolve","SWEPT_BODY",BODY,{"disambiguationData":[OSD([sQuery(id+"F0.wireOp",EDGE,"E1")])]}),"instanceName":"1"}),"instanceName":"1"}),"instanceName":"1"}),"instanceName":"1"}),"instanceName":"1"}),"instanceName":"1"});
            var Q1672;
            Q1672=makeQuery(id+"F13.opPattern","COPY",BODY,{"derivedFrom":makeQuery(id+"F9.opPattern","COPY",BODY,{"derivedFrom":makeQuery(id+"F7.opPattern","COPY",BODY,{"derivedFrom":makeQuery(id+"F6.opPattern","COPY",BODY,{"derivedFrom":makeQuery(id+"F4.opPattern","COPY",BODY,{"derivedFrom":makeQuery(id+"F3.opPattern","COPY",BODY,{"derivedFrom":makeQuery(id+"F2.opPattern","COPY",BODY,{"derivedFrom":makeQuery(id+"F1.opRevolve","SWEPT_BODY",BODY,{"disambiguationData":[OSD([sQuery(id+"F0.wireOp",EDGE,"E1")])]}),"instanceName":"1"}),"instanceName":"1"}),"instanceName":"1"}),"instanceName":"1"}),"instanceName":"1"}),"instanceName":"1"}),"instanceName":"1"});
            var Q1673;
            Q1673=makeQuery(id+"F13.opPattern","COPY",BODY,{"derivedFrom":makeQuery(id+"F9.opPattern","COPY",BODY,{"derivedFrom":makeQuery(id+"F7.opPattern","COPY",BODY,{"derivedFrom":makeQuery(id+"F6.opPattern","COPY",BODY,{"derivedFrom":makeQuery(id+"F5.opPattern","COPY",BODY,{"derivedFrom":makeQuery(id+"F1.opRevolve","SWEPT_BODY",BODY,{"disambiguationData":[OSD([sQuery(id+"F0.wireOp",EDGE,"E1")])]}),"instanceName":"1"}),"instanceName":"1"}),"instanceName":"1"}),"instanceName":"1"}),"instanceName":"1"});
            var Q1674;
            Q1674=makeQuery(id+"F13.opPattern","COPY",BODY,{"derivedFrom":makeQuery(id+"F9.opPattern","COPY",BODY,{"derivedFrom":makeQuery(id+"F7.opPattern","COPY",BODY,{"derivedFrom":makeQuery(id+"F6.opPattern","COPY",BODY,{"derivedFrom":makeQuery(id+"F5.opPattern","COPY",BODY,{"derivedFrom":makeQuery(id+"F2.opPattern","COPY",BODY,{"derivedFrom":makeQuery(id+"F1.opRevolve","SWEPT_BODY",BODY,{"disambiguationData":[OSD([sQuery(id+"F0.wireOp",EDGE,"E1")])]}),"instanceName":"1"}),"instanceName":"1"}),"instanceName":"1"}),"instanceName":"1"}),"instanceName":"1"}),"instanceName":"1"});
            var Q1675;
            Q1675=makeQuery(id+"F13.opPattern","COPY",BODY,{"derivedFrom":makeQuery(id+"F9.opPattern","COPY",BODY,{"derivedFrom":makeQuery(id+"F7.opPattern","COPY",BODY,{"derivedFrom":makeQuery(id+"F6.opPattern","COPY",BODY,{"derivedFrom":makeQuery(id+"F5.opPattern","COPY",BODY,{"derivedFrom":makeQuery(id+"F3.opPattern","COPY",BODY,{"derivedFrom":makeQuery(id+"F2.opPattern","COPY",BODY,{"derivedFrom":makeQuery(id+"F1.opRevolve","SWEPT_BODY",BODY,{"disambiguationData":[OSD([sQuery(id+"F0.wireOp",EDGE,"E1")])]}),"instanceName":"1"}),"instanceName":"1"}),"instanceName":"1"}),"instanceName":"1"}),"instanceName":"1"}),"instanceName":"1"}),"instanceName":"1"});
            var Q1676;
            Q1676=makeQuery(id+"F13.opPattern","COPY",BODY,{"derivedFrom":makeQuery(id+"F9.opPattern","COPY",BODY,{"derivedFrom":makeQuery(id+"F7.opPattern","COPY",BODY,{"derivedFrom":makeQuery(id+"F6.opPattern","COPY",BODY,{"derivedFrom":makeQuery(id+"F5.opPattern","COPY",BODY,{"derivedFrom":makeQuery(id+"F4.opPattern","COPY",BODY,{"derivedFrom":makeQuery(id+"F1.opRevolve","SWEPT_BODY",BODY,{"disambiguationData":[OSD([sQuery(id+"F0.wireOp",EDGE,"E1")])]}),"instanceName":"1"}),"instanceName":"1"}),"instanceName":"1"}),"instanceName":"1"}),"instanceName":"1"}),"instanceName":"1"});
            var Q1677;
            Q1677=makeQuery(id+"F13.opPattern","COPY",BODY,{"derivedFrom":makeQuery(id+"F9.opPattern","COPY",BODY,{"derivedFrom":makeQuery(id+"F7.opPattern","COPY",BODY,{"derivedFrom":makeQuery(id+"F6.opPattern","COPY",BODY,{"derivedFrom":makeQuery(id+"F5.opPattern","COPY",BODY,{"derivedFrom":makeQuery(id+"F4.opPattern","COPY",BODY,{"derivedFrom":makeQuery(id+"F2.opPattern","COPY",BODY,{"derivedFrom":makeQuery(id+"F1.opRevolve","SWEPT_BODY",BODY,{"disambiguationData":[OSD([sQuery(id+"F0.wireOp",EDGE,"E1")])]}),"instanceName":"1"}),"instanceName":"1"}),"instanceName":"1"}),"instanceName":"1"}),"instanceName":"1"}),"instanceName":"1"}),"instanceName":"1"});
            var Q1678;
            Q1678=makeQuery(id+"F13.opPattern","COPY",BODY,{"derivedFrom":makeQuery(id+"F9.opPattern","COPY",BODY,{"derivedFrom":makeQuery(id+"F7.opPattern","COPY",BODY,{"derivedFrom":makeQuery(id+"F6.opPattern","COPY",BODY,{"derivedFrom":makeQuery(id+"F5.opPattern","COPY",BODY,{"derivedFrom":makeQuery(id+"F4.opPattern","COPY",BODY,{"derivedFrom":makeQuery(id+"F3.opPattern","COPY",BODY,{"derivedFrom":makeQuery(id+"F2.opPattern","COPY",BODY,{"derivedFrom":makeQuery(id+"F1.opRevolve","SWEPT_BODY",BODY,{"disambiguationData":[OSD([sQuery(id+"F0.wireOp",EDGE,"E1")])]}),"instanceName":"1"}),"instanceName":"1"}),"instanceName":"1"}),"instanceName":"1"}),"instanceName":"1"}),"instanceName":"1"}),"instanceName":"1"}),"instanceName":"1"});
            var Q1679;
            Q1679=makeQuery(id+"F13.opPattern","COPY",BODY,{"derivedFrom":makeQuery(id+"F9.opPattern","COPY",BODY,{"derivedFrom":makeQuery(id+"F8.opPattern","COPY",BODY,{"derivedFrom":makeQuery(id+"F1.opRevolve","SWEPT_BODY",BODY,{"disambiguationData":[OSD([sQuery(id+"F0.wireOp",EDGE,"E1")])]}),"instanceName":"1"}),"instanceName":"1"}),"instanceName":"1"});
            var Q1680;
            Q1680=makeQuery(id+"F13.opPattern","COPY",BODY,{"derivedFrom":makeQuery(id+"F9.opPattern","COPY",BODY,{"derivedFrom":makeQuery(id+"F8.opPattern","COPY",BODY,{"derivedFrom":makeQuery(id+"F2.opPattern","COPY",BODY,{"derivedFrom":makeQuery(id+"F1.opRevolve","SWEPT_BODY",BODY,{"disambiguationData":[OSD([sQuery(id+"F0.wireOp",EDGE,"E1")])]}),"instanceName":"1"}),"instanceName":"1"}),"instanceName":"1"}),"instanceName":"1"});
            var Q1681;
            Q1681=makeQuery(id+"F13.opPattern","COPY",BODY,{"derivedFrom":makeQuery(id+"F9.opPattern","COPY",BODY,{"derivedFrom":makeQuery(id+"F8.opPattern","COPY",BODY,{"derivedFrom":makeQuery(id+"F3.opPattern","COPY",BODY,{"derivedFrom":makeQuery(id+"F2.opPattern","COPY",BODY,{"derivedFrom":makeQuery(id+"F1.opRevolve","SWEPT_BODY",BODY,{"disambiguationData":[OSD([sQuery(id+"F0.wireOp",EDGE,"E1")])]}),"instanceName":"1"}),"instanceName":"1"}),"instanceName":"1"}),"instanceName":"1"}),"instanceName":"1"});
            var Q1682;
            Q1682=makeQuery(id+"F13.opPattern","COPY",BODY,{"derivedFrom":makeQuery(id+"F9.opPattern","COPY",BODY,{"derivedFrom":makeQuery(id+"F8.opPattern","COPY",BODY,{"derivedFrom":makeQuery(id+"F4.opPattern","COPY",BODY,{"derivedFrom":makeQuery(id+"F1.opRevolve","SWEPT_BODY",BODY,{"disambiguationData":[OSD([sQuery(id+"F0.wireOp",EDGE,"E1")])]}),"instanceName":"1"}),"instanceName":"1"}),"instanceName":"1"}),"instanceName":"1"});
            var Q1683;
            Q1683=makeQuery(id+"F13.opPattern","COPY",BODY,{"derivedFrom":makeQuery(id+"F9.opPattern","COPY",BODY,{"derivedFrom":makeQuery(id+"F8.opPattern","COPY",BODY,{"derivedFrom":makeQuery(id+"F4.opPattern","COPY",BODY,{"derivedFrom":makeQuery(id+"F2.opPattern","COPY",BODY,{"derivedFrom":makeQuery(id+"F1.opRevolve","SWEPT_BODY",BODY,{"disambiguationData":[OSD([sQuery(id+"F0.wireOp",EDGE,"E1")])]}),"instanceName":"1"}),"instanceName":"1"}),"instanceName":"1"}),"instanceName":"1"}),"instanceName":"1"});
            var Q1684;
            Q1684=makeQuery(id+"F13.opPattern","COPY",BODY,{"derivedFrom":makeQuery(id+"F9.opPattern","COPY",BODY,{"derivedFrom":makeQuery(id+"F8.opPattern","COPY",BODY,{"derivedFrom":makeQuery(id+"F4.opPattern","COPY",BODY,{"derivedFrom":makeQuery(id+"F3.opPattern","COPY",BODY,{"derivedFrom":makeQuery(id+"F2.opPattern","COPY",BODY,{"derivedFrom":makeQuery(id+"F1.opRevolve","SWEPT_BODY",BODY,{"disambiguationData":[OSD([sQuery(id+"F0.wireOp",EDGE,"E1")])]}),"instanceName":"1"}),"instanceName":"1"}),"instanceName":"1"}),"instanceName":"1"}),"instanceName":"1"}),"instanceName":"1"});
            var Q1685;
            Q1685=makeQuery(id+"F13.opPattern","COPY",BODY,{"derivedFrom":makeQuery(id+"F9.opPattern","COPY",BODY,{"derivedFrom":makeQuery(id+"F8.opPattern","COPY",BODY,{"derivedFrom":makeQuery(id+"F5.opPattern","COPY",BODY,{"derivedFrom":makeQuery(id+"F1.opRevolve","SWEPT_BODY",BODY,{"disambiguationData":[OSD([sQuery(id+"F0.wireOp",EDGE,"E1")])]}),"instanceName":"1"}),"instanceName":"1"}),"instanceName":"1"}),"instanceName":"1"});
            var Q1686;
            Q1686=makeQuery(id+"F13.opPattern","COPY",BODY,{"derivedFrom":makeQuery(id+"F9.opPattern","COPY",BODY,{"derivedFrom":makeQuery(id+"F8.opPattern","COPY",BODY,{"derivedFrom":makeQuery(id+"F5.opPattern","COPY",BODY,{"derivedFrom":makeQuery(id+"F2.opPattern","COPY",BODY,{"derivedFrom":makeQuery(id+"F1.opRevolve","SWEPT_BODY",BODY,{"disambiguationData":[OSD([sQuery(id+"F0.wireOp",EDGE,"E1")])]}),"instanceName":"1"}),"instanceName":"1"}),"instanceName":"1"}),"instanceName":"1"}),"instanceName":"1"});
            var Q1687;
            Q1687=makeQuery(id+"F13.opPattern","COPY",BODY,{"derivedFrom":makeQuery(id+"F9.opPattern","COPY",BODY,{"derivedFrom":makeQuery(id+"F8.opPattern","COPY",BODY,{"derivedFrom":makeQuery(id+"F5.opPattern","COPY",BODY,{"derivedFrom":makeQuery(id+"F3.opPattern","COPY",BODY,{"derivedFrom":makeQuery(id+"F2.opPattern","COPY",BODY,{"derivedFrom":makeQuery(id+"F1.opRevolve","SWEPT_BODY",BODY,{"disambiguationData":[OSD([sQuery(id+"F0.wireOp",EDGE,"E1")])]}),"instanceName":"1"}),"instanceName":"1"}),"instanceName":"1"}),"instanceName":"1"}),"instanceName":"1"}),"instanceName":"1"});
            var Q1688;
            Q1688=makeQuery(id+"F13.opPattern","COPY",BODY,{"derivedFrom":makeQuery(id+"F9.opPattern","COPY",BODY,{"derivedFrom":makeQuery(id+"F8.opPattern","COPY",BODY,{"derivedFrom":makeQuery(id+"F5.opPattern","COPY",BODY,{"derivedFrom":makeQuery(id+"F4.opPattern","COPY",BODY,{"derivedFrom":makeQuery(id+"F1.opRevolve","SWEPT_BODY",BODY,{"disambiguationData":[OSD([sQuery(id+"F0.wireOp",EDGE,"E1")])]}),"instanceName":"1"}),"instanceName":"1"}),"instanceName":"1"}),"instanceName":"1"}),"instanceName":"1"});
            var Q1689;
            Q1689=makeQuery(id+"F13.opPattern","COPY",BODY,{"derivedFrom":makeQuery(id+"F9.opPattern","COPY",BODY,{"derivedFrom":makeQuery(id+"F8.opPattern","COPY",BODY,{"derivedFrom":makeQuery(id+"F5.opPattern","COPY",BODY,{"derivedFrom":makeQuery(id+"F4.opPattern","COPY",BODY,{"derivedFrom":makeQuery(id+"F2.opPattern","COPY",BODY,{"derivedFrom":makeQuery(id+"F1.opRevolve","SWEPT_BODY",BODY,{"disambiguationData":[OSD([sQuery(id+"F0.wireOp",EDGE,"E1")])]}),"instanceName":"1"}),"instanceName":"1"}),"instanceName":"1"}),"instanceName":"1"}),"instanceName":"1"}),"instanceName":"1"});
            var Q1690;
            Q1690=makeQuery(id+"F13.opPattern","COPY",BODY,{"derivedFrom":makeQuery(id+"F9.opPattern","COPY",BODY,{"derivedFrom":makeQuery(id+"F8.opPattern","COPY",BODY,{"derivedFrom":makeQuery(id+"F5.opPattern","COPY",BODY,{"derivedFrom":makeQuery(id+"F4.opPattern","COPY",BODY,{"derivedFrom":makeQuery(id+"F3.opPattern","COPY",BODY,{"derivedFrom":makeQuery(id+"F2.opPattern","COPY",BODY,{"derivedFrom":makeQuery(id+"F1.opRevolve","SWEPT_BODY",BODY,{"disambiguationData":[OSD([sQuery(id+"F0.wireOp",EDGE,"E1")])]}),"instanceName":"1"}),"instanceName":"1"}),"instanceName":"1"}),"instanceName":"1"}),"instanceName":"1"}),"instanceName":"1"}),"instanceName":"1"});
            var Q1691;
            Q1691=makeQuery(id+"F13.opPattern","COPY",BODY,{"derivedFrom":makeQuery(id+"F9.opPattern","COPY",BODY,{"derivedFrom":makeQuery(id+"F8.opPattern","COPY",BODY,{"derivedFrom":makeQuery(id+"F6.opPattern","COPY",BODY,{"derivedFrom":makeQuery(id+"F1.opRevolve","SWEPT_BODY",BODY,{"disambiguationData":[OSD([sQuery(id+"F0.wireOp",EDGE,"E1")])]}),"instanceName":"1"}),"instanceName":"1"}),"instanceName":"1"}),"instanceName":"1"});
            var Q1692;
            Q1692=makeQuery(id+"F13.opPattern","COPY",BODY,{"derivedFrom":makeQuery(id+"F9.opPattern","COPY",BODY,{"derivedFrom":makeQuery(id+"F8.opPattern","COPY",BODY,{"derivedFrom":makeQuery(id+"F6.opPattern","COPY",BODY,{"derivedFrom":makeQuery(id+"F2.opPattern","COPY",BODY,{"derivedFrom":makeQuery(id+"F1.opRevolve","SWEPT_BODY",BODY,{"disambiguationData":[OSD([sQuery(id+"F0.wireOp",EDGE,"E1")])]}),"instanceName":"1"}),"instanceName":"1"}),"instanceName":"1"}),"instanceName":"1"}),"instanceName":"1"});
            var Q1693;
            Q1693=makeQuery(id+"F13.opPattern","COPY",BODY,{"derivedFrom":makeQuery(id+"F9.opPattern","COPY",BODY,{"derivedFrom":makeQuery(id+"F8.opPattern","COPY",BODY,{"derivedFrom":makeQuery(id+"F6.opPattern","COPY",BODY,{"derivedFrom":makeQuery(id+"F3.opPattern","COPY",BODY,{"derivedFrom":makeQuery(id+"F2.opPattern","COPY",BODY,{"derivedFrom":makeQuery(id+"F1.opRevolve","SWEPT_BODY",BODY,{"disambiguationData":[OSD([sQuery(id+"F0.wireOp",EDGE,"E1")])]}),"instanceName":"1"}),"instanceName":"1"}),"instanceName":"1"}),"instanceName":"1"}),"instanceName":"1"}),"instanceName":"1"});
            var Q1694;
            Q1694=makeQuery(id+"F13.opPattern","COPY",BODY,{"derivedFrom":makeQuery(id+"F9.opPattern","COPY",BODY,{"derivedFrom":makeQuery(id+"F8.opPattern","COPY",BODY,{"derivedFrom":makeQuery(id+"F6.opPattern","COPY",BODY,{"derivedFrom":makeQuery(id+"F4.opPattern","COPY",BODY,{"derivedFrom":makeQuery(id+"F1.opRevolve","SWEPT_BODY",BODY,{"disambiguationData":[OSD([sQuery(id+"F0.wireOp",EDGE,"E1")])]}),"instanceName":"1"}),"instanceName":"1"}),"instanceName":"1"}),"instanceName":"1"}),"instanceName":"1"});
            var Q1695;
            Q1695=makeQuery(id+"F13.opPattern","COPY",BODY,{"derivedFrom":makeQuery(id+"F9.opPattern","COPY",BODY,{"derivedFrom":makeQuery(id+"F8.opPattern","COPY",BODY,{"derivedFrom":makeQuery(id+"F6.opPattern","COPY",BODY,{"derivedFrom":makeQuery(id+"F4.opPattern","COPY",BODY,{"derivedFrom":makeQuery(id+"F2.opPattern","COPY",BODY,{"derivedFrom":makeQuery(id+"F1.opRevolve","SWEPT_BODY",BODY,{"disambiguationData":[OSD([sQuery(id+"F0.wireOp",EDGE,"E1")])]}),"instanceName":"1"}),"instanceName":"1"}),"instanceName":"1"}),"instanceName":"1"}),"instanceName":"1"}),"instanceName":"1"});
            var Q1696;
            Q1696=makeQuery(id+"F13.opPattern","COPY",BODY,{"derivedFrom":makeQuery(id+"F9.opPattern","COPY",BODY,{"derivedFrom":makeQuery(id+"F8.opPattern","COPY",BODY,{"derivedFrom":makeQuery(id+"F6.opPattern","COPY",BODY,{"derivedFrom":makeQuery(id+"F4.opPattern","COPY",BODY,{"derivedFrom":makeQuery(id+"F3.opPattern","COPY",BODY,{"derivedFrom":makeQuery(id+"F2.opPattern","COPY",BODY,{"derivedFrom":makeQuery(id+"F1.opRevolve","SWEPT_BODY",BODY,{"disambiguationData":[OSD([sQuery(id+"F0.wireOp",EDGE,"E1")])]}),"instanceName":"1"}),"instanceName":"1"}),"instanceName":"1"}),"instanceName":"1"}),"instanceName":"1"}),"instanceName":"1"}),"instanceName":"1"});
            var Q1697;
            Q1697=makeQuery(id+"F13.opPattern","COPY",BODY,{"derivedFrom":makeQuery(id+"F9.opPattern","COPY",BODY,{"derivedFrom":makeQuery(id+"F8.opPattern","COPY",BODY,{"derivedFrom":makeQuery(id+"F6.opPattern","COPY",BODY,{"derivedFrom":makeQuery(id+"F5.opPattern","COPY",BODY,{"derivedFrom":makeQuery(id+"F1.opRevolve","SWEPT_BODY",BODY,{"disambiguationData":[OSD([sQuery(id+"F0.wireOp",EDGE,"E1")])]}),"instanceName":"1"}),"instanceName":"1"}),"instanceName":"1"}),"instanceName":"1"}),"instanceName":"1"});
            var Q1698;
            Q1698=makeQuery(id+"F13.opPattern","COPY",BODY,{"derivedFrom":makeQuery(id+"F9.opPattern","COPY",BODY,{"derivedFrom":makeQuery(id+"F8.opPattern","COPY",BODY,{"derivedFrom":makeQuery(id+"F6.opPattern","COPY",BODY,{"derivedFrom":makeQuery(id+"F5.opPattern","COPY",BODY,{"derivedFrom":makeQuery(id+"F2.opPattern","COPY",BODY,{"derivedFrom":makeQuery(id+"F1.opRevolve","SWEPT_BODY",BODY,{"disambiguationData":[OSD([sQuery(id+"F0.wireOp",EDGE,"E1")])]}),"instanceName":"1"}),"instanceName":"1"}),"instanceName":"1"}),"instanceName":"1"}),"instanceName":"1"}),"instanceName":"1"});
            var Q1699;
            Q1699=makeQuery(id+"F13.opPattern","COPY",BODY,{"derivedFrom":makeQuery(id+"F9.opPattern","COPY",BODY,{"derivedFrom":makeQuery(id+"F8.opPattern","COPY",BODY,{"derivedFrom":makeQuery(id+"F6.opPattern","COPY",BODY,{"derivedFrom":makeQuery(id+"F5.opPattern","COPY",BODY,{"derivedFrom":makeQuery(id+"F3.opPattern","COPY",BODY,{"derivedFrom":makeQuery(id+"F2.opPattern","COPY",BODY,{"derivedFrom":makeQuery(id+"F1.opRevolve","SWEPT_BODY",BODY,{"disambiguationData":[OSD([sQuery(id+"F0.wireOp",EDGE,"E1")])]}),"instanceName":"1"}),"instanceName":"1"}),"instanceName":"1"}),"instanceName":"1"}),"instanceName":"1"}),"instanceName":"1"}),"instanceName":"1"});
            var Q1700;
            Q1700=makeQuery(id+"F13.opPattern","COPY",BODY,{"derivedFrom":makeQuery(id+"F9.opPattern","COPY",BODY,{"derivedFrom":makeQuery(id+"F8.opPattern","COPY",BODY,{"derivedFrom":makeQuery(id+"F6.opPattern","COPY",BODY,{"derivedFrom":makeQuery(id+"F5.opPattern","COPY",BODY,{"derivedFrom":makeQuery(id+"F4.opPattern","COPY",BODY,{"derivedFrom":makeQuery(id+"F1.opRevolve","SWEPT_BODY",BODY,{"disambiguationData":[OSD([sQuery(id+"F0.wireOp",EDGE,"E1")])]}),"instanceName":"1"}),"instanceName":"1"}),"instanceName":"1"}),"instanceName":"1"}),"instanceName":"1"}),"instanceName":"1"});
            var Q1701;
            Q1701=makeQuery(id+"F13.opPattern","COPY",BODY,{"derivedFrom":makeQuery(id+"F9.opPattern","COPY",BODY,{"derivedFrom":makeQuery(id+"F8.opPattern","COPY",BODY,{"derivedFrom":makeQuery(id+"F6.opPattern","COPY",BODY,{"derivedFrom":makeQuery(id+"F5.opPattern","COPY",BODY,{"derivedFrom":makeQuery(id+"F4.opPattern","COPY",BODY,{"derivedFrom":makeQuery(id+"F2.opPattern","COPY",BODY,{"derivedFrom":makeQuery(id+"F1.opRevolve","SWEPT_BODY",BODY,{"disambiguationData":[OSD([sQuery(id+"F0.wireOp",EDGE,"E1")])]}),"instanceName":"1"}),"instanceName":"1"}),"instanceName":"1"}),"instanceName":"1"}),"instanceName":"1"}),"instanceName":"1"}),"instanceName":"1"});
            var Q1702;
            Q1702=makeQuery(id+"F13.opPattern","COPY",BODY,{"derivedFrom":makeQuery(id+"F9.opPattern","COPY",BODY,{"derivedFrom":makeQuery(id+"F8.opPattern","COPY",BODY,{"derivedFrom":makeQuery(id+"F6.opPattern","COPY",BODY,{"derivedFrom":makeQuery(id+"F5.opPattern","COPY",BODY,{"derivedFrom":makeQuery(id+"F4.opPattern","COPY",BODY,{"derivedFrom":makeQuery(id+"F3.opPattern","COPY",BODY,{"derivedFrom":makeQuery(id+"F2.opPattern","COPY",BODY,{"derivedFrom":makeQuery(id+"F1.opRevolve","SWEPT_BODY",BODY,{"disambiguationData":[OSD([sQuery(id+"F0.wireOp",EDGE,"E1")])]}),"instanceName":"1"}),"instanceName":"1"}),"instanceName":"1"}),"instanceName":"1"}),"instanceName":"1"}),"instanceName":"1"}),"instanceName":"1"}),"instanceName":"1"});
            var Q1703;
            Q1703=makeQuery(id+"F13.opPattern","COPY",BODY,{"derivedFrom":makeQuery(id+"F9.opPattern","COPY",BODY,{"derivedFrom":makeQuery(id+"F8.opPattern","COPY",BODY,{"derivedFrom":makeQuery(id+"F7.opPattern","COPY",BODY,{"derivedFrom":makeQuery(id+"F1.opRevolve","SWEPT_BODY",BODY,{"disambiguationData":[OSD([sQuery(id+"F0.wireOp",EDGE,"E1")])]}),"instanceName":"1"}),"instanceName":"1"}),"instanceName":"1"}),"instanceName":"1"});
            var Q1704;
            Q1704=makeQuery(id+"F13.opPattern","COPY",BODY,{"derivedFrom":makeQuery(id+"F9.opPattern","COPY",BODY,{"derivedFrom":makeQuery(id+"F8.opPattern","COPY",BODY,{"derivedFrom":makeQuery(id+"F7.opPattern","COPY",BODY,{"derivedFrom":makeQuery(id+"F2.opPattern","COPY",BODY,{"derivedFrom":makeQuery(id+"F1.opRevolve","SWEPT_BODY",BODY,{"disambiguationData":[OSD([sQuery(id+"F0.wireOp",EDGE,"E1")])]}),"instanceName":"1"}),"instanceName":"1"}),"instanceName":"1"}),"instanceName":"1"}),"instanceName":"1"});
            var Q1705;
            Q1705=makeQuery(id+"F13.opPattern","COPY",BODY,{"derivedFrom":makeQuery(id+"F9.opPattern","COPY",BODY,{"derivedFrom":makeQuery(id+"F8.opPattern","COPY",BODY,{"derivedFrom":makeQuery(id+"F7.opPattern","COPY",BODY,{"derivedFrom":makeQuery(id+"F3.opPattern","COPY",BODY,{"derivedFrom":makeQuery(id+"F2.opPattern","COPY",BODY,{"derivedFrom":makeQuery(id+"F1.opRevolve","SWEPT_BODY",BODY,{"disambiguationData":[OSD([sQuery(id+"F0.wireOp",EDGE,"E1")])]}),"instanceName":"1"}),"instanceName":"1"}),"instanceName":"1"}),"instanceName":"1"}),"instanceName":"1"}),"instanceName":"1"});
            var Q1706;
            Q1706=makeQuery(id+"F13.opPattern","COPY",BODY,{"derivedFrom":makeQuery(id+"F9.opPattern","COPY",BODY,{"derivedFrom":makeQuery(id+"F8.opPattern","COPY",BODY,{"derivedFrom":makeQuery(id+"F7.opPattern","COPY",BODY,{"derivedFrom":makeQuery(id+"F4.opPattern","COPY",BODY,{"derivedFrom":makeQuery(id+"F1.opRevolve","SWEPT_BODY",BODY,{"disambiguationData":[OSD([sQuery(id+"F0.wireOp",EDGE,"E1")])]}),"instanceName":"1"}),"instanceName":"1"}),"instanceName":"1"}),"instanceName":"1"}),"instanceName":"1"});
            var Q1707;
            Q1707=makeQuery(id+"F13.opPattern","COPY",BODY,{"derivedFrom":makeQuery(id+"F9.opPattern","COPY",BODY,{"derivedFrom":makeQuery(id+"F8.opPattern","COPY",BODY,{"derivedFrom":makeQuery(id+"F7.opPattern","COPY",BODY,{"derivedFrom":makeQuery(id+"F4.opPattern","COPY",BODY,{"derivedFrom":makeQuery(id+"F2.opPattern","COPY",BODY,{"derivedFrom":makeQuery(id+"F1.opRevolve","SWEPT_BODY",BODY,{"disambiguationData":[OSD([sQuery(id+"F0.wireOp",EDGE,"E1")])]}),"instanceName":"1"}),"instanceName":"1"}),"instanceName":"1"}),"instanceName":"1"}),"instanceName":"1"}),"instanceName":"1"});
            var Q1708;
            Q1708=makeQuery(id+"F13.opPattern","COPY",BODY,{"derivedFrom":makeQuery(id+"F9.opPattern","COPY",BODY,{"derivedFrom":makeQuery(id+"F8.opPattern","COPY",BODY,{"derivedFrom":makeQuery(id+"F7.opPattern","COPY",BODY,{"derivedFrom":makeQuery(id+"F4.opPattern","COPY",BODY,{"derivedFrom":makeQuery(id+"F3.opPattern","COPY",BODY,{"derivedFrom":makeQuery(id+"F2.opPattern","COPY",BODY,{"derivedFrom":makeQuery(id+"F1.opRevolve","SWEPT_BODY",BODY,{"disambiguationData":[OSD([sQuery(id+"F0.wireOp",EDGE,"E1")])]}),"instanceName":"1"}),"instanceName":"1"}),"instanceName":"1"}),"instanceName":"1"}),"instanceName":"1"}),"instanceName":"1"}),"instanceName":"1"});
            var Q1709;
            Q1709=makeQuery(id+"F13.opPattern","COPY",BODY,{"derivedFrom":makeQuery(id+"F9.opPattern","COPY",BODY,{"derivedFrom":makeQuery(id+"F8.opPattern","COPY",BODY,{"derivedFrom":makeQuery(id+"F7.opPattern","COPY",BODY,{"derivedFrom":makeQuery(id+"F5.opPattern","COPY",BODY,{"derivedFrom":makeQuery(id+"F1.opRevolve","SWEPT_BODY",BODY,{"disambiguationData":[OSD([sQuery(id+"F0.wireOp",EDGE,"E1")])]}),"instanceName":"1"}),"instanceName":"1"}),"instanceName":"1"}),"instanceName":"1"}),"instanceName":"1"});
            var Q1710;
            Q1710=makeQuery(id+"F13.opPattern","COPY",BODY,{"derivedFrom":makeQuery(id+"F9.opPattern","COPY",BODY,{"derivedFrom":makeQuery(id+"F8.opPattern","COPY",BODY,{"derivedFrom":makeQuery(id+"F7.opPattern","COPY",BODY,{"derivedFrom":makeQuery(id+"F5.opPattern","COPY",BODY,{"derivedFrom":makeQuery(id+"F2.opPattern","COPY",BODY,{"derivedFrom":makeQuery(id+"F1.opRevolve","SWEPT_BODY",BODY,{"disambiguationData":[OSD([sQuery(id+"F0.wireOp",EDGE,"E1")])]}),"instanceName":"1"}),"instanceName":"1"}),"instanceName":"1"}),"instanceName":"1"}),"instanceName":"1"}),"instanceName":"1"});
            var Q1711;
            Q1711=makeQuery(id+"F13.opPattern","COPY",BODY,{"derivedFrom":makeQuery(id+"F9.opPattern","COPY",BODY,{"derivedFrom":makeQuery(id+"F8.opPattern","COPY",BODY,{"derivedFrom":makeQuery(id+"F7.opPattern","COPY",BODY,{"derivedFrom":makeQuery(id+"F5.opPattern","COPY",BODY,{"derivedFrom":makeQuery(id+"F3.opPattern","COPY",BODY,{"derivedFrom":makeQuery(id+"F2.opPattern","COPY",BODY,{"derivedFrom":makeQuery(id+"F1.opRevolve","SWEPT_BODY",BODY,{"disambiguationData":[OSD([sQuery(id+"F0.wireOp",EDGE,"E1")])]}),"instanceName":"1"}),"instanceName":"1"}),"instanceName":"1"}),"instanceName":"1"}),"instanceName":"1"}),"instanceName":"1"}),"instanceName":"1"});
            var Q1712;
            Q1712=makeQuery(id+"F13.opPattern","COPY",BODY,{"derivedFrom":makeQuery(id+"F9.opPattern","COPY",BODY,{"derivedFrom":makeQuery(id+"F8.opPattern","COPY",BODY,{"derivedFrom":makeQuery(id+"F7.opPattern","COPY",BODY,{"derivedFrom":makeQuery(id+"F5.opPattern","COPY",BODY,{"derivedFrom":makeQuery(id+"F4.opPattern","COPY",BODY,{"derivedFrom":makeQuery(id+"F1.opRevolve","SWEPT_BODY",BODY,{"disambiguationData":[OSD([sQuery(id+"F0.wireOp",EDGE,"E1")])]}),"instanceName":"1"}),"instanceName":"1"}),"instanceName":"1"}),"instanceName":"1"}),"instanceName":"1"}),"instanceName":"1"});
            var Q1713;
            Q1713=makeQuery(id+"F13.opPattern","COPY",BODY,{"derivedFrom":makeQuery(id+"F9.opPattern","COPY",BODY,{"derivedFrom":makeQuery(id+"F8.opPattern","COPY",BODY,{"derivedFrom":makeQuery(id+"F7.opPattern","COPY",BODY,{"derivedFrom":makeQuery(id+"F5.opPattern","COPY",BODY,{"derivedFrom":makeQuery(id+"F4.opPattern","COPY",BODY,{"derivedFrom":makeQuery(id+"F2.opPattern","COPY",BODY,{"derivedFrom":makeQuery(id+"F1.opRevolve","SWEPT_BODY",BODY,{"disambiguationData":[OSD([sQuery(id+"F0.wireOp",EDGE,"E1")])]}),"instanceName":"1"}),"instanceName":"1"}),"instanceName":"1"}),"instanceName":"1"}),"instanceName":"1"}),"instanceName":"1"}),"instanceName":"1"});
            var Q1714;
            Q1714=makeQuery(id+"F13.opPattern","COPY",BODY,{"derivedFrom":makeQuery(id+"F9.opPattern","COPY",BODY,{"derivedFrom":makeQuery(id+"F8.opPattern","COPY",BODY,{"derivedFrom":makeQuery(id+"F7.opPattern","COPY",BODY,{"derivedFrom":makeQuery(id+"F5.opPattern","COPY",BODY,{"derivedFrom":makeQuery(id+"F4.opPattern","COPY",BODY,{"derivedFrom":makeQuery(id+"F3.opPattern","COPY",BODY,{"derivedFrom":makeQuery(id+"F2.opPattern","COPY",BODY,{"derivedFrom":makeQuery(id+"F1.opRevolve","SWEPT_BODY",BODY,{"disambiguationData":[OSD([sQuery(id+"F0.wireOp",EDGE,"E1")])]}),"instanceName":"1"}),"instanceName":"1"}),"instanceName":"1"}),"instanceName":"1"}),"instanceName":"1"}),"instanceName":"1"}),"instanceName":"1"}),"instanceName":"1"});
            var Q1715;
            Q1715=makeQuery(id+"F13.opPattern","COPY",BODY,{"derivedFrom":makeQuery(id+"F9.opPattern","COPY",BODY,{"derivedFrom":makeQuery(id+"F8.opPattern","COPY",BODY,{"derivedFrom":makeQuery(id+"F7.opPattern","COPY",BODY,{"derivedFrom":makeQuery(id+"F6.opPattern","COPY",BODY,{"derivedFrom":makeQuery(id+"F1.opRevolve","SWEPT_BODY",BODY,{"disambiguationData":[OSD([sQuery(id+"F0.wireOp",EDGE,"E1")])]}),"instanceName":"1"}),"instanceName":"1"}),"instanceName":"1"}),"instanceName":"1"}),"instanceName":"1"});
            var Q1716;
            Q1716=makeQuery(id+"F13.opPattern","COPY",BODY,{"derivedFrom":makeQuery(id+"F9.opPattern","COPY",BODY,{"derivedFrom":makeQuery(id+"F8.opPattern","COPY",BODY,{"derivedFrom":makeQuery(id+"F7.opPattern","COPY",BODY,{"derivedFrom":makeQuery(id+"F6.opPattern","COPY",BODY,{"derivedFrom":makeQuery(id+"F2.opPattern","COPY",BODY,{"derivedFrom":makeQuery(id+"F1.opRevolve","SWEPT_BODY",BODY,{"disambiguationData":[OSD([sQuery(id+"F0.wireOp",EDGE,"E1")])]}),"instanceName":"1"}),"instanceName":"1"}),"instanceName":"1"}),"instanceName":"1"}),"instanceName":"1"}),"instanceName":"1"});
            var Q1717;
            Q1717=makeQuery(id+"F13.opPattern","COPY",BODY,{"derivedFrom":makeQuery(id+"F9.opPattern","COPY",BODY,{"derivedFrom":makeQuery(id+"F8.opPattern","COPY",BODY,{"derivedFrom":makeQuery(id+"F7.opPattern","COPY",BODY,{"derivedFrom":makeQuery(id+"F6.opPattern","COPY",BODY,{"derivedFrom":makeQuery(id+"F3.opPattern","COPY",BODY,{"derivedFrom":makeQuery(id+"F2.opPattern","COPY",BODY,{"derivedFrom":makeQuery(id+"F1.opRevolve","SWEPT_BODY",BODY,{"disambiguationData":[OSD([sQuery(id+"F0.wireOp",EDGE,"E1")])]}),"instanceName":"1"}),"instanceName":"1"}),"instanceName":"1"}),"instanceName":"1"}),"instanceName":"1"}),"instanceName":"1"}),"instanceName":"1"});
            var Q1718;
            Q1718=makeQuery(id+"F13.opPattern","COPY",BODY,{"derivedFrom":makeQuery(id+"F9.opPattern","COPY",BODY,{"derivedFrom":makeQuery(id+"F8.opPattern","COPY",BODY,{"derivedFrom":makeQuery(id+"F7.opPattern","COPY",BODY,{"derivedFrom":makeQuery(id+"F6.opPattern","COPY",BODY,{"derivedFrom":makeQuery(id+"F4.opPattern","COPY",BODY,{"derivedFrom":makeQuery(id+"F1.opRevolve","SWEPT_BODY",BODY,{"disambiguationData":[OSD([sQuery(id+"F0.wireOp",EDGE,"E1")])]}),"instanceName":"1"}),"instanceName":"1"}),"instanceName":"1"}),"instanceName":"1"}),"instanceName":"1"}),"instanceName":"1"});
            var Q1719;
            Q1719=makeQuery(id+"F13.opPattern","COPY",BODY,{"derivedFrom":makeQuery(id+"F9.opPattern","COPY",BODY,{"derivedFrom":makeQuery(id+"F8.opPattern","COPY",BODY,{"derivedFrom":makeQuery(id+"F7.opPattern","COPY",BODY,{"derivedFrom":makeQuery(id+"F6.opPattern","COPY",BODY,{"derivedFrom":makeQuery(id+"F4.opPattern","COPY",BODY,{"derivedFrom":makeQuery(id+"F2.opPattern","COPY",BODY,{"derivedFrom":makeQuery(id+"F1.opRevolve","SWEPT_BODY",BODY,{"disambiguationData":[OSD([sQuery(id+"F0.wireOp",EDGE,"E1")])]}),"instanceName":"1"}),"instanceName":"1"}),"instanceName":"1"}),"instanceName":"1"}),"instanceName":"1"}),"instanceName":"1"}),"instanceName":"1"});
            var Q1720;
            Q1720=makeQuery(id+"F13.opPattern","COPY",BODY,{"derivedFrom":makeQuery(id+"F9.opPattern","COPY",BODY,{"derivedFrom":makeQuery(id+"F8.opPattern","COPY",BODY,{"derivedFrom":makeQuery(id+"F7.opPattern","COPY",BODY,{"derivedFrom":makeQuery(id+"F6.opPattern","COPY",BODY,{"derivedFrom":makeQuery(id+"F4.opPattern","COPY",BODY,{"derivedFrom":makeQuery(id+"F3.opPattern","COPY",BODY,{"derivedFrom":makeQuery(id+"F2.opPattern","COPY",BODY,{"derivedFrom":makeQuery(id+"F1.opRevolve","SWEPT_BODY",BODY,{"disambiguationData":[OSD([sQuery(id+"F0.wireOp",EDGE,"E1")])]}),"instanceName":"1"}),"instanceName":"1"}),"instanceName":"1"}),"instanceName":"1"}),"instanceName":"1"}),"instanceName":"1"}),"instanceName":"1"}),"instanceName":"1"});
            var Q1721;
            Q1721=makeQuery(id+"F13.opPattern","COPY",BODY,{"derivedFrom":makeQuery(id+"F9.opPattern","COPY",BODY,{"derivedFrom":makeQuery(id+"F8.opPattern","COPY",BODY,{"derivedFrom":makeQuery(id+"F7.opPattern","COPY",BODY,{"derivedFrom":makeQuery(id+"F6.opPattern","COPY",BODY,{"derivedFrom":makeQuery(id+"F5.opPattern","COPY",BODY,{"derivedFrom":makeQuery(id+"F1.opRevolve","SWEPT_BODY",BODY,{"disambiguationData":[OSD([sQuery(id+"F0.wireOp",EDGE,"E1")])]}),"instanceName":"1"}),"instanceName":"1"}),"instanceName":"1"}),"instanceName":"1"}),"instanceName":"1"}),"instanceName":"1"});
            var Q1722;
            Q1722=makeQuery(id+"F13.opPattern","COPY",BODY,{"derivedFrom":makeQuery(id+"F9.opPattern","COPY",BODY,{"derivedFrom":makeQuery(id+"F8.opPattern","COPY",BODY,{"derivedFrom":makeQuery(id+"F7.opPattern","COPY",BODY,{"derivedFrom":makeQuery(id+"F6.opPattern","COPY",BODY,{"derivedFrom":makeQuery(id+"F5.opPattern","COPY",BODY,{"derivedFrom":makeQuery(id+"F2.opPattern","COPY",BODY,{"derivedFrom":makeQuery(id+"F1.opRevolve","SWEPT_BODY",BODY,{"disambiguationData":[OSD([sQuery(id+"F0.wireOp",EDGE,"E1")])]}),"instanceName":"1"}),"instanceName":"1"}),"instanceName":"1"}),"instanceName":"1"}),"instanceName":"1"}),"instanceName":"1"}),"instanceName":"1"});
            var Q1723;
            Q1723=makeQuery(id+"F13.opPattern","COPY",BODY,{"derivedFrom":makeQuery(id+"F9.opPattern","COPY",BODY,{"derivedFrom":makeQuery(id+"F8.opPattern","COPY",BODY,{"derivedFrom":makeQuery(id+"F7.opPattern","COPY",BODY,{"derivedFrom":makeQuery(id+"F6.opPattern","COPY",BODY,{"derivedFrom":makeQuery(id+"F5.opPattern","COPY",BODY,{"derivedFrom":makeQuery(id+"F3.opPattern","COPY",BODY,{"derivedFrom":makeQuery(id+"F2.opPattern","COPY",BODY,{"derivedFrom":makeQuery(id+"F1.opRevolve","SWEPT_BODY",BODY,{"disambiguationData":[OSD([sQuery(id+"F0.wireOp",EDGE,"E1")])]}),"instanceName":"1"}),"instanceName":"1"}),"instanceName":"1"}),"instanceName":"1"}),"instanceName":"1"}),"instanceName":"1"}),"instanceName":"1"}),"instanceName":"1"});
            var Q1724;
            Q1724=makeQuery(id+"F13.opPattern","COPY",BODY,{"derivedFrom":makeQuery(id+"F9.opPattern","COPY",BODY,{"derivedFrom":makeQuery(id+"F8.opPattern","COPY",BODY,{"derivedFrom":makeQuery(id+"F7.opPattern","COPY",BODY,{"derivedFrom":makeQuery(id+"F6.opPattern","COPY",BODY,{"derivedFrom":makeQuery(id+"F5.opPattern","COPY",BODY,{"derivedFrom":makeQuery(id+"F4.opPattern","COPY",BODY,{"derivedFrom":makeQuery(id+"F1.opRevolve","SWEPT_BODY",BODY,{"disambiguationData":[OSD([sQuery(id+"F0.wireOp",EDGE,"E1")])]}),"instanceName":"1"}),"instanceName":"1"}),"instanceName":"1"}),"instanceName":"1"}),"instanceName":"1"}),"instanceName":"1"}),"instanceName":"1"});
            var Q1725;
            Q1725=makeQuery(id+"F13.opPattern","COPY",BODY,{"derivedFrom":makeQuery(id+"F9.opPattern","COPY",BODY,{"derivedFrom":makeQuery(id+"F8.opPattern","COPY",BODY,{"derivedFrom":makeQuery(id+"F7.opPattern","COPY",BODY,{"derivedFrom":makeQuery(id+"F6.opPattern","COPY",BODY,{"derivedFrom":makeQuery(id+"F5.opPattern","COPY",BODY,{"derivedFrom":makeQuery(id+"F4.opPattern","COPY",BODY,{"derivedFrom":makeQuery(id+"F2.opPattern","COPY",BODY,{"derivedFrom":makeQuery(id+"F1.opRevolve","SWEPT_BODY",BODY,{"disambiguationData":[OSD([sQuery(id+"F0.wireOp",EDGE,"E1")])]}),"instanceName":"1"}),"instanceName":"1"}),"instanceName":"1"}),"instanceName":"1"}),"instanceName":"1"}),"instanceName":"1"}),"instanceName":"1"}),"instanceName":"1"});
            var Q1726;
            Q1726=makeQuery(id+"F13.opPattern","COPY",BODY,{"derivedFrom":makeQuery(id+"F9.opPattern","COPY",BODY,{"derivedFrom":makeQuery(id+"F8.opPattern","COPY",BODY,{"derivedFrom":makeQuery(id+"F7.opPattern","COPY",BODY,{"derivedFrom":makeQuery(id+"F6.opPattern","COPY",BODY,{"derivedFrom":makeQuery(id+"F5.opPattern","COPY",BODY,{"derivedFrom":makeQuery(id+"F4.opPattern","COPY",BODY,{"derivedFrom":makeQuery(id+"F3.opPattern","COPY",BODY,{"derivedFrom":makeQuery(id+"F2.opPattern","COPY",BODY,{"derivedFrom":makeQuery(id+"F1.opRevolve","SWEPT_BODY",BODY,{"disambiguationData":[OSD([sQuery(id+"F0.wireOp",EDGE,"E1")])]}),"instanceName":"1"}),"instanceName":"1"}),"instanceName":"1"}),"instanceName":"1"}),"instanceName":"1"}),"instanceName":"1"}),"instanceName":"1"}),"instanceName":"1"}),"instanceName":"1"});
            var Q1727;
            Q1727=makeQuery(id+"F13.opPattern","COPY",BODY,{"derivedFrom":makeQuery(id+"F10.opPattern","COPY",BODY,{"derivedFrom":makeQuery(id+"F1.opRevolve","SWEPT_BODY",BODY,{"disambiguationData":[OSD([sQuery(id+"F0.wireOp",EDGE,"E1")])]}),"instanceName":"1"}),"instanceName":"1"});
            var Q1728;
            Q1728=makeQuery(id+"F13.opPattern","COPY",BODY,{"derivedFrom":makeQuery(id+"F10.opPattern","COPY",BODY,{"derivedFrom":makeQuery(id+"F2.opPattern","COPY",BODY,{"derivedFrom":makeQuery(id+"F1.opRevolve","SWEPT_BODY",BODY,{"disambiguationData":[OSD([sQuery(id+"F0.wireOp",EDGE,"E1")])]}),"instanceName":"1"}),"instanceName":"1"}),"instanceName":"1"});
            var Q1729;
            Q1729=makeQuery(id+"F13.opPattern","COPY",BODY,{"derivedFrom":makeQuery(id+"F10.opPattern","COPY",BODY,{"derivedFrom":makeQuery(id+"F3.opPattern","COPY",BODY,{"derivedFrom":makeQuery(id+"F2.opPattern","COPY",BODY,{"derivedFrom":makeQuery(id+"F1.opRevolve","SWEPT_BODY",BODY,{"disambiguationData":[OSD([sQuery(id+"F0.wireOp",EDGE,"E1")])]}),"instanceName":"1"}),"instanceName":"1"}),"instanceName":"1"}),"instanceName":"1"});
            var Q1730;
            Q1730=makeQuery(id+"F13.opPattern","COPY",BODY,{"derivedFrom":makeQuery(id+"F10.opPattern","COPY",BODY,{"derivedFrom":makeQuery(id+"F4.opPattern","COPY",BODY,{"derivedFrom":makeQuery(id+"F1.opRevolve","SWEPT_BODY",BODY,{"disambiguationData":[OSD([sQuery(id+"F0.wireOp",EDGE,"E1")])]}),"instanceName":"1"}),"instanceName":"1"}),"instanceName":"1"});
            var Q1731;
            Q1731=makeQuery(id+"F13.opPattern","COPY",BODY,{"derivedFrom":makeQuery(id+"F10.opPattern","COPY",BODY,{"derivedFrom":makeQuery(id+"F4.opPattern","COPY",BODY,{"derivedFrom":makeQuery(id+"F2.opPattern","COPY",BODY,{"derivedFrom":makeQuery(id+"F1.opRevolve","SWEPT_BODY",BODY,{"disambiguationData":[OSD([sQuery(id+"F0.wireOp",EDGE,"E1")])]}),"instanceName":"1"}),"instanceName":"1"}),"instanceName":"1"}),"instanceName":"1"});
            var Q1732;
            Q1732=makeQuery(id+"F13.opPattern","COPY",BODY,{"derivedFrom":makeQuery(id+"F10.opPattern","COPY",BODY,{"derivedFrom":makeQuery(id+"F4.opPattern","COPY",BODY,{"derivedFrom":makeQuery(id+"F3.opPattern","COPY",BODY,{"derivedFrom":makeQuery(id+"F2.opPattern","COPY",BODY,{"derivedFrom":makeQuery(id+"F1.opRevolve","SWEPT_BODY",BODY,{"disambiguationData":[OSD([sQuery(id+"F0.wireOp",EDGE,"E1")])]}),"instanceName":"1"}),"instanceName":"1"}),"instanceName":"1"}),"instanceName":"1"}),"instanceName":"1"});
            var Q1733;
            Q1733=makeQuery(id+"F13.opPattern","COPY",BODY,{"derivedFrom":makeQuery(id+"F10.opPattern","COPY",BODY,{"derivedFrom":makeQuery(id+"F5.opPattern","COPY",BODY,{"derivedFrom":makeQuery(id+"F1.opRevolve","SWEPT_BODY",BODY,{"disambiguationData":[OSD([sQuery(id+"F0.wireOp",EDGE,"E1")])]}),"instanceName":"1"}),"instanceName":"1"}),"instanceName":"1"});
            var Q1734;
            Q1734=makeQuery(id+"F13.opPattern","COPY",BODY,{"derivedFrom":makeQuery(id+"F10.opPattern","COPY",BODY,{"derivedFrom":makeQuery(id+"F5.opPattern","COPY",BODY,{"derivedFrom":makeQuery(id+"F2.opPattern","COPY",BODY,{"derivedFrom":makeQuery(id+"F1.opRevolve","SWEPT_BODY",BODY,{"disambiguationData":[OSD([sQuery(id+"F0.wireOp",EDGE,"E1")])]}),"instanceName":"1"}),"instanceName":"1"}),"instanceName":"1"}),"instanceName":"1"});
            var Q1735;
            Q1735=makeQuery(id+"F13.opPattern","COPY",BODY,{"derivedFrom":makeQuery(id+"F10.opPattern","COPY",BODY,{"derivedFrom":makeQuery(id+"F5.opPattern","COPY",BODY,{"derivedFrom":makeQuery(id+"F3.opPattern","COPY",BODY,{"derivedFrom":makeQuery(id+"F2.opPattern","COPY",BODY,{"derivedFrom":makeQuery(id+"F1.opRevolve","SWEPT_BODY",BODY,{"disambiguationData":[OSD([sQuery(id+"F0.wireOp",EDGE,"E1")])]}),"instanceName":"1"}),"instanceName":"1"}),"instanceName":"1"}),"instanceName":"1"}),"instanceName":"1"});
            var Q1736;
            Q1736=makeQuery(id+"F13.opPattern","COPY",BODY,{"derivedFrom":makeQuery(id+"F10.opPattern","COPY",BODY,{"derivedFrom":makeQuery(id+"F5.opPattern","COPY",BODY,{"derivedFrom":makeQuery(id+"F4.opPattern","COPY",BODY,{"derivedFrom":makeQuery(id+"F1.opRevolve","SWEPT_BODY",BODY,{"disambiguationData":[OSD([sQuery(id+"F0.wireOp",EDGE,"E1")])]}),"instanceName":"1"}),"instanceName":"1"}),"instanceName":"1"}),"instanceName":"1"});
            var Q1737;
            Q1737=makeQuery(id+"F13.opPattern","COPY",BODY,{"derivedFrom":makeQuery(id+"F10.opPattern","COPY",BODY,{"derivedFrom":makeQuery(id+"F5.opPattern","COPY",BODY,{"derivedFrom":makeQuery(id+"F4.opPattern","COPY",BODY,{"derivedFrom":makeQuery(id+"F2.opPattern","COPY",BODY,{"derivedFrom":makeQuery(id+"F1.opRevolve","SWEPT_BODY",BODY,{"disambiguationData":[OSD([sQuery(id+"F0.wireOp",EDGE,"E1")])]}),"instanceName":"1"}),"instanceName":"1"}),"instanceName":"1"}),"instanceName":"1"}),"instanceName":"1"});
            var Q1738;
            Q1738=makeQuery(id+"F13.opPattern","COPY",BODY,{"derivedFrom":makeQuery(id+"F10.opPattern","COPY",BODY,{"derivedFrom":makeQuery(id+"F5.opPattern","COPY",BODY,{"derivedFrom":makeQuery(id+"F4.opPattern","COPY",BODY,{"derivedFrom":makeQuery(id+"F3.opPattern","COPY",BODY,{"derivedFrom":makeQuery(id+"F2.opPattern","COPY",BODY,{"derivedFrom":makeQuery(id+"F1.opRevolve","SWEPT_BODY",BODY,{"disambiguationData":[OSD([sQuery(id+"F0.wireOp",EDGE,"E1")])]}),"instanceName":"1"}),"instanceName":"1"}),"instanceName":"1"}),"instanceName":"1"}),"instanceName":"1"}),"instanceName":"1"});
            var Q1739;
            Q1739=makeQuery(id+"F13.opPattern","COPY",BODY,{"derivedFrom":makeQuery(id+"F10.opPattern","COPY",BODY,{"derivedFrom":makeQuery(id+"F6.opPattern","COPY",BODY,{"derivedFrom":makeQuery(id+"F1.opRevolve","SWEPT_BODY",BODY,{"disambiguationData":[OSD([sQuery(id+"F0.wireOp",EDGE,"E1")])]}),"instanceName":"1"}),"instanceName":"1"}),"instanceName":"1"});
            var Q1740;
            Q1740=makeQuery(id+"F13.opPattern","COPY",BODY,{"derivedFrom":makeQuery(id+"F10.opPattern","COPY",BODY,{"derivedFrom":makeQuery(id+"F6.opPattern","COPY",BODY,{"derivedFrom":makeQuery(id+"F2.opPattern","COPY",BODY,{"derivedFrom":makeQuery(id+"F1.opRevolve","SWEPT_BODY",BODY,{"disambiguationData":[OSD([sQuery(id+"F0.wireOp",EDGE,"E1")])]}),"instanceName":"1"}),"instanceName":"1"}),"instanceName":"1"}),"instanceName":"1"});
            var Q1741;
            Q1741=makeQuery(id+"F13.opPattern","COPY",BODY,{"derivedFrom":makeQuery(id+"F10.opPattern","COPY",BODY,{"derivedFrom":makeQuery(id+"F6.opPattern","COPY",BODY,{"derivedFrom":makeQuery(id+"F3.opPattern","COPY",BODY,{"derivedFrom":makeQuery(id+"F2.opPattern","COPY",BODY,{"derivedFrom":makeQuery(id+"F1.opRevolve","SWEPT_BODY",BODY,{"disambiguationData":[OSD([sQuery(id+"F0.wireOp",EDGE,"E1")])]}),"instanceName":"1"}),"instanceName":"1"}),"instanceName":"1"}),"instanceName":"1"}),"instanceName":"1"});
            var Q1742;
            Q1742=makeQuery(id+"F13.opPattern","COPY",BODY,{"derivedFrom":makeQuery(id+"F10.opPattern","COPY",BODY,{"derivedFrom":makeQuery(id+"F6.opPattern","COPY",BODY,{"derivedFrom":makeQuery(id+"F4.opPattern","COPY",BODY,{"derivedFrom":makeQuery(id+"F1.opRevolve","SWEPT_BODY",BODY,{"disambiguationData":[OSD([sQuery(id+"F0.wireOp",EDGE,"E1")])]}),"instanceName":"1"}),"instanceName":"1"}),"instanceName":"1"}),"instanceName":"1"});
            var Q1743;
            Q1743=makeQuery(id+"F13.opPattern","COPY",BODY,{"derivedFrom":makeQuery(id+"F10.opPattern","COPY",BODY,{"derivedFrom":makeQuery(id+"F6.opPattern","COPY",BODY,{"derivedFrom":makeQuery(id+"F4.opPattern","COPY",BODY,{"derivedFrom":makeQuery(id+"F2.opPattern","COPY",BODY,{"derivedFrom":makeQuery(id+"F1.opRevolve","SWEPT_BODY",BODY,{"disambiguationData":[OSD([sQuery(id+"F0.wireOp",EDGE,"E1")])]}),"instanceName":"1"}),"instanceName":"1"}),"instanceName":"1"}),"instanceName":"1"}),"instanceName":"1"});
            var Q1744;
            Q1744=makeQuery(id+"F13.opPattern","COPY",BODY,{"derivedFrom":makeQuery(id+"F10.opPattern","COPY",BODY,{"derivedFrom":makeQuery(id+"F6.opPattern","COPY",BODY,{"derivedFrom":makeQuery(id+"F4.opPattern","COPY",BODY,{"derivedFrom":makeQuery(id+"F3.opPattern","COPY",BODY,{"derivedFrom":makeQuery(id+"F2.opPattern","COPY",BODY,{"derivedFrom":makeQuery(id+"F1.opRevolve","SWEPT_BODY",BODY,{"disambiguationData":[OSD([sQuery(id+"F0.wireOp",EDGE,"E1")])]}),"instanceName":"1"}),"instanceName":"1"}),"instanceName":"1"}),"instanceName":"1"}),"instanceName":"1"}),"instanceName":"1"});
            var Q1745;
            Q1745=makeQuery(id+"F13.opPattern","COPY",BODY,{"derivedFrom":makeQuery(id+"F10.opPattern","COPY",BODY,{"derivedFrom":makeQuery(id+"F6.opPattern","COPY",BODY,{"derivedFrom":makeQuery(id+"F5.opPattern","COPY",BODY,{"derivedFrom":makeQuery(id+"F1.opRevolve","SWEPT_BODY",BODY,{"disambiguationData":[OSD([sQuery(id+"F0.wireOp",EDGE,"E1")])]}),"instanceName":"1"}),"instanceName":"1"}),"instanceName":"1"}),"instanceName":"1"});
            var Q1746;
            Q1746=makeQuery(id+"F13.opPattern","COPY",BODY,{"derivedFrom":makeQuery(id+"F10.opPattern","COPY",BODY,{"derivedFrom":makeQuery(id+"F6.opPattern","COPY",BODY,{"derivedFrom":makeQuery(id+"F5.opPattern","COPY",BODY,{"derivedFrom":makeQuery(id+"F2.opPattern","COPY",BODY,{"derivedFrom":makeQuery(id+"F1.opRevolve","SWEPT_BODY",BODY,{"disambiguationData":[OSD([sQuery(id+"F0.wireOp",EDGE,"E1")])]}),"instanceName":"1"}),"instanceName":"1"}),"instanceName":"1"}),"instanceName":"1"}),"instanceName":"1"});
            var Q1747;
            Q1747=makeQuery(id+"F13.opPattern","COPY",BODY,{"derivedFrom":makeQuery(id+"F10.opPattern","COPY",BODY,{"derivedFrom":makeQuery(id+"F6.opPattern","COPY",BODY,{"derivedFrom":makeQuery(id+"F5.opPattern","COPY",BODY,{"derivedFrom":makeQuery(id+"F3.opPattern","COPY",BODY,{"derivedFrom":makeQuery(id+"F2.opPattern","COPY",BODY,{"derivedFrom":makeQuery(id+"F1.opRevolve","SWEPT_BODY",BODY,{"disambiguationData":[OSD([sQuery(id+"F0.wireOp",EDGE,"E1")])]}),"instanceName":"1"}),"instanceName":"1"}),"instanceName":"1"}),"instanceName":"1"}),"instanceName":"1"}),"instanceName":"1"});
            var Q1748;
            Q1748=makeQuery(id+"F13.opPattern","COPY",BODY,{"derivedFrom":makeQuery(id+"F10.opPattern","COPY",BODY,{"derivedFrom":makeQuery(id+"F6.opPattern","COPY",BODY,{"derivedFrom":makeQuery(id+"F5.opPattern","COPY",BODY,{"derivedFrom":makeQuery(id+"F4.opPattern","COPY",BODY,{"derivedFrom":makeQuery(id+"F1.opRevolve","SWEPT_BODY",BODY,{"disambiguationData":[OSD([sQuery(id+"F0.wireOp",EDGE,"E1")])]}),"instanceName":"1"}),"instanceName":"1"}),"instanceName":"1"}),"instanceName":"1"}),"instanceName":"1"});
            var Q1749;
            Q1749=makeQuery(id+"F13.opPattern","COPY",BODY,{"derivedFrom":makeQuery(id+"F10.opPattern","COPY",BODY,{"derivedFrom":makeQuery(id+"F6.opPattern","COPY",BODY,{"derivedFrom":makeQuery(id+"F5.opPattern","COPY",BODY,{"derivedFrom":makeQuery(id+"F4.opPattern","COPY",BODY,{"derivedFrom":makeQuery(id+"F2.opPattern","COPY",BODY,{"derivedFrom":makeQuery(id+"F1.opRevolve","SWEPT_BODY",BODY,{"disambiguationData":[OSD([sQuery(id+"F0.wireOp",EDGE,"E1")])]}),"instanceName":"1"}),"instanceName":"1"}),"instanceName":"1"}),"instanceName":"1"}),"instanceName":"1"}),"instanceName":"1"});
            var Q1750;
            Q1750=makeQuery(id+"F13.opPattern","COPY",BODY,{"derivedFrom":makeQuery(id+"F10.opPattern","COPY",BODY,{"derivedFrom":makeQuery(id+"F6.opPattern","COPY",BODY,{"derivedFrom":makeQuery(id+"F5.opPattern","COPY",BODY,{"derivedFrom":makeQuery(id+"F4.opPattern","COPY",BODY,{"derivedFrom":makeQuery(id+"F3.opPattern","COPY",BODY,{"derivedFrom":makeQuery(id+"F2.opPattern","COPY",BODY,{"derivedFrom":makeQuery(id+"F1.opRevolve","SWEPT_BODY",BODY,{"disambiguationData":[OSD([sQuery(id+"F0.wireOp",EDGE,"E1")])]}),"instanceName":"1"}),"instanceName":"1"}),"instanceName":"1"}),"instanceName":"1"}),"instanceName":"1"}),"instanceName":"1"}),"instanceName":"1"});
            var Q1751;
            Q1751=makeQuery(id+"F13.opPattern","COPY",BODY,{"derivedFrom":makeQuery(id+"F10.opPattern","COPY",BODY,{"derivedFrom":makeQuery(id+"F7.opPattern","COPY",BODY,{"derivedFrom":makeQuery(id+"F1.opRevolve","SWEPT_BODY",BODY,{"disambiguationData":[OSD([sQuery(id+"F0.wireOp",EDGE,"E1")])]}),"instanceName":"1"}),"instanceName":"1"}),"instanceName":"1"});
            var Q1752;
            Q1752=makeQuery(id+"F13.opPattern","COPY",BODY,{"derivedFrom":makeQuery(id+"F10.opPattern","COPY",BODY,{"derivedFrom":makeQuery(id+"F7.opPattern","COPY",BODY,{"derivedFrom":makeQuery(id+"F2.opPattern","COPY",BODY,{"derivedFrom":makeQuery(id+"F1.opRevolve","SWEPT_BODY",BODY,{"disambiguationData":[OSD([sQuery(id+"F0.wireOp",EDGE,"E1")])]}),"instanceName":"1"}),"instanceName":"1"}),"instanceName":"1"}),"instanceName":"1"});
            var Q1753;
            Q1753=makeQuery(id+"F13.opPattern","COPY",BODY,{"derivedFrom":makeQuery(id+"F10.opPattern","COPY",BODY,{"derivedFrom":makeQuery(id+"F7.opPattern","COPY",BODY,{"derivedFrom":makeQuery(id+"F3.opPattern","COPY",BODY,{"derivedFrom":makeQuery(id+"F2.opPattern","COPY",BODY,{"derivedFrom":makeQuery(id+"F1.opRevolve","SWEPT_BODY",BODY,{"disambiguationData":[OSD([sQuery(id+"F0.wireOp",EDGE,"E1")])]}),"instanceName":"1"}),"instanceName":"1"}),"instanceName":"1"}),"instanceName":"1"}),"instanceName":"1"});
            var Q1754;
            Q1754=makeQuery(id+"F13.opPattern","COPY",BODY,{"derivedFrom":makeQuery(id+"F10.opPattern","COPY",BODY,{"derivedFrom":makeQuery(id+"F7.opPattern","COPY",BODY,{"derivedFrom":makeQuery(id+"F4.opPattern","COPY",BODY,{"derivedFrom":makeQuery(id+"F1.opRevolve","SWEPT_BODY",BODY,{"disambiguationData":[OSD([sQuery(id+"F0.wireOp",EDGE,"E1")])]}),"instanceName":"1"}),"instanceName":"1"}),"instanceName":"1"}),"instanceName":"1"});
            var Q1755;
            Q1755=makeQuery(id+"F13.opPattern","COPY",BODY,{"derivedFrom":makeQuery(id+"F10.opPattern","COPY",BODY,{"derivedFrom":makeQuery(id+"F7.opPattern","COPY",BODY,{"derivedFrom":makeQuery(id+"F4.opPattern","COPY",BODY,{"derivedFrom":makeQuery(id+"F2.opPattern","COPY",BODY,{"derivedFrom":makeQuery(id+"F1.opRevolve","SWEPT_BODY",BODY,{"disambiguationData":[OSD([sQuery(id+"F0.wireOp",EDGE,"E1")])]}),"instanceName":"1"}),"instanceName":"1"}),"instanceName":"1"}),"instanceName":"1"}),"instanceName":"1"});
            var Q1756;
            Q1756=makeQuery(id+"F13.opPattern","COPY",BODY,{"derivedFrom":makeQuery(id+"F10.opPattern","COPY",BODY,{"derivedFrom":makeQuery(id+"F7.opPattern","COPY",BODY,{"derivedFrom":makeQuery(id+"F4.opPattern","COPY",BODY,{"derivedFrom":makeQuery(id+"F3.opPattern","COPY",BODY,{"derivedFrom":makeQuery(id+"F2.opPattern","COPY",BODY,{"derivedFrom":makeQuery(id+"F1.opRevolve","SWEPT_BODY",BODY,{"disambiguationData":[OSD([sQuery(id+"F0.wireOp",EDGE,"E1")])]}),"instanceName":"1"}),"instanceName":"1"}),"instanceName":"1"}),"instanceName":"1"}),"instanceName":"1"}),"instanceName":"1"});
            var Q1757;
            Q1757=makeQuery(id+"F13.opPattern","COPY",BODY,{"derivedFrom":makeQuery(id+"F10.opPattern","COPY",BODY,{"derivedFrom":makeQuery(id+"F7.opPattern","COPY",BODY,{"derivedFrom":makeQuery(id+"F5.opPattern","COPY",BODY,{"derivedFrom":makeQuery(id+"F1.opRevolve","SWEPT_BODY",BODY,{"disambiguationData":[OSD([sQuery(id+"F0.wireOp",EDGE,"E1")])]}),"instanceName":"1"}),"instanceName":"1"}),"instanceName":"1"}),"instanceName":"1"});
            var Q1758;
            Q1758=makeQuery(id+"F13.opPattern","COPY",BODY,{"derivedFrom":makeQuery(id+"F10.opPattern","COPY",BODY,{"derivedFrom":makeQuery(id+"F7.opPattern","COPY",BODY,{"derivedFrom":makeQuery(id+"F5.opPattern","COPY",BODY,{"derivedFrom":makeQuery(id+"F2.opPattern","COPY",BODY,{"derivedFrom":makeQuery(id+"F1.opRevolve","SWEPT_BODY",BODY,{"disambiguationData":[OSD([sQuery(id+"F0.wireOp",EDGE,"E1")])]}),"instanceName":"1"}),"instanceName":"1"}),"instanceName":"1"}),"instanceName":"1"}),"instanceName":"1"});
            var Q1759;
            Q1759=makeQuery(id+"F13.opPattern","COPY",BODY,{"derivedFrom":makeQuery(id+"F10.opPattern","COPY",BODY,{"derivedFrom":makeQuery(id+"F7.opPattern","COPY",BODY,{"derivedFrom":makeQuery(id+"F5.opPattern","COPY",BODY,{"derivedFrom":makeQuery(id+"F3.opPattern","COPY",BODY,{"derivedFrom":makeQuery(id+"F2.opPattern","COPY",BODY,{"derivedFrom":makeQuery(id+"F1.opRevolve","SWEPT_BODY",BODY,{"disambiguationData":[OSD([sQuery(id+"F0.wireOp",EDGE,"E1")])]}),"instanceName":"1"}),"instanceName":"1"}),"instanceName":"1"}),"instanceName":"1"}),"instanceName":"1"}),"instanceName":"1"});
            var Q1760;
            Q1760=makeQuery(id+"F13.opPattern","COPY",BODY,{"derivedFrom":makeQuery(id+"F10.opPattern","COPY",BODY,{"derivedFrom":makeQuery(id+"F7.opPattern","COPY",BODY,{"derivedFrom":makeQuery(id+"F5.opPattern","COPY",BODY,{"derivedFrom":makeQuery(id+"F4.opPattern","COPY",BODY,{"derivedFrom":makeQuery(id+"F1.opRevolve","SWEPT_BODY",BODY,{"disambiguationData":[OSD([sQuery(id+"F0.wireOp",EDGE,"E1")])]}),"instanceName":"1"}),"instanceName":"1"}),"instanceName":"1"}),"instanceName":"1"}),"instanceName":"1"});
            var Q1761;
            Q1761=makeQuery(id+"F13.opPattern","COPY",BODY,{"derivedFrom":makeQuery(id+"F10.opPattern","COPY",BODY,{"derivedFrom":makeQuery(id+"F7.opPattern","COPY",BODY,{"derivedFrom":makeQuery(id+"F5.opPattern","COPY",BODY,{"derivedFrom":makeQuery(id+"F4.opPattern","COPY",BODY,{"derivedFrom":makeQuery(id+"F2.opPattern","COPY",BODY,{"derivedFrom":makeQuery(id+"F1.opRevolve","SWEPT_BODY",BODY,{"disambiguationData":[OSD([sQuery(id+"F0.wireOp",EDGE,"E1")])]}),"instanceName":"1"}),"instanceName":"1"}),"instanceName":"1"}),"instanceName":"1"}),"instanceName":"1"}),"instanceName":"1"});
            var Q1762;
            Q1762=makeQuery(id+"F13.opPattern","COPY",BODY,{"derivedFrom":makeQuery(id+"F10.opPattern","COPY",BODY,{"derivedFrom":makeQuery(id+"F7.opPattern","COPY",BODY,{"derivedFrom":makeQuery(id+"F5.opPattern","COPY",BODY,{"derivedFrom":makeQuery(id+"F4.opPattern","COPY",BODY,{"derivedFrom":makeQuery(id+"F3.opPattern","COPY",BODY,{"derivedFrom":makeQuery(id+"F2.opPattern","COPY",BODY,{"derivedFrom":makeQuery(id+"F1.opRevolve","SWEPT_BODY",BODY,{"disambiguationData":[OSD([sQuery(id+"F0.wireOp",EDGE,"E1")])]}),"instanceName":"1"}),"instanceName":"1"}),"instanceName":"1"}),"instanceName":"1"}),"instanceName":"1"}),"instanceName":"1"}),"instanceName":"1"});
            var Q1763;
            Q1763=makeQuery(id+"F13.opPattern","COPY",BODY,{"derivedFrom":makeQuery(id+"F10.opPattern","COPY",BODY,{"derivedFrom":makeQuery(id+"F7.opPattern","COPY",BODY,{"derivedFrom":makeQuery(id+"F6.opPattern","COPY",BODY,{"derivedFrom":makeQuery(id+"F1.opRevolve","SWEPT_BODY",BODY,{"disambiguationData":[OSD([sQuery(id+"F0.wireOp",EDGE,"E1")])]}),"instanceName":"1"}),"instanceName":"1"}),"instanceName":"1"}),"instanceName":"1"});
            var Q1764;
            Q1764=makeQuery(id+"F13.opPattern","COPY",BODY,{"derivedFrom":makeQuery(id+"F10.opPattern","COPY",BODY,{"derivedFrom":makeQuery(id+"F7.opPattern","COPY",BODY,{"derivedFrom":makeQuery(id+"F6.opPattern","COPY",BODY,{"derivedFrom":makeQuery(id+"F2.opPattern","COPY",BODY,{"derivedFrom":makeQuery(id+"F1.opRevolve","SWEPT_BODY",BODY,{"disambiguationData":[OSD([sQuery(id+"F0.wireOp",EDGE,"E1")])]}),"instanceName":"1"}),"instanceName":"1"}),"instanceName":"1"}),"instanceName":"1"}),"instanceName":"1"});
            var Q1765;
            Q1765=makeQuery(id+"F13.opPattern","COPY",BODY,{"derivedFrom":makeQuery(id+"F10.opPattern","COPY",BODY,{"derivedFrom":makeQuery(id+"F7.opPattern","COPY",BODY,{"derivedFrom":makeQuery(id+"F6.opPattern","COPY",BODY,{"derivedFrom":makeQuery(id+"F3.opPattern","COPY",BODY,{"derivedFrom":makeQuery(id+"F2.opPattern","COPY",BODY,{"derivedFrom":makeQuery(id+"F1.opRevolve","SWEPT_BODY",BODY,{"disambiguationData":[OSD([sQuery(id+"F0.wireOp",EDGE,"E1")])]}),"instanceName":"1"}),"instanceName":"1"}),"instanceName":"1"}),"instanceName":"1"}),"instanceName":"1"}),"instanceName":"1"});
            var Q1766;
            Q1766=makeQuery(id+"F13.opPattern","COPY",BODY,{"derivedFrom":makeQuery(id+"F10.opPattern","COPY",BODY,{"derivedFrom":makeQuery(id+"F7.opPattern","COPY",BODY,{"derivedFrom":makeQuery(id+"F6.opPattern","COPY",BODY,{"derivedFrom":makeQuery(id+"F4.opPattern","COPY",BODY,{"derivedFrom":makeQuery(id+"F1.opRevolve","SWEPT_BODY",BODY,{"disambiguationData":[OSD([sQuery(id+"F0.wireOp",EDGE,"E1")])]}),"instanceName":"1"}),"instanceName":"1"}),"instanceName":"1"}),"instanceName":"1"}),"instanceName":"1"});
            var Q1767;
            Q1767=makeQuery(id+"F13.opPattern","COPY",BODY,{"derivedFrom":makeQuery(id+"F10.opPattern","COPY",BODY,{"derivedFrom":makeQuery(id+"F7.opPattern","COPY",BODY,{"derivedFrom":makeQuery(id+"F6.opPattern","COPY",BODY,{"derivedFrom":makeQuery(id+"F4.opPattern","COPY",BODY,{"derivedFrom":makeQuery(id+"F2.opPattern","COPY",BODY,{"derivedFrom":makeQuery(id+"F1.opRevolve","SWEPT_BODY",BODY,{"disambiguationData":[OSD([sQuery(id+"F0.wireOp",EDGE,"E1")])]}),"instanceName":"1"}),"instanceName":"1"}),"instanceName":"1"}),"instanceName":"1"}),"instanceName":"1"}),"instanceName":"1"});
            var Q1768;
            Q1768=makeQuery(id+"F13.opPattern","COPY",BODY,{"derivedFrom":makeQuery(id+"F10.opPattern","COPY",BODY,{"derivedFrom":makeQuery(id+"F7.opPattern","COPY",BODY,{"derivedFrom":makeQuery(id+"F6.opPattern","COPY",BODY,{"derivedFrom":makeQuery(id+"F4.opPattern","COPY",BODY,{"derivedFrom":makeQuery(id+"F3.opPattern","COPY",BODY,{"derivedFrom":makeQuery(id+"F2.opPattern","COPY",BODY,{"derivedFrom":makeQuery(id+"F1.opRevolve","SWEPT_BODY",BODY,{"disambiguationData":[OSD([sQuery(id+"F0.wireOp",EDGE,"E1")])]}),"instanceName":"1"}),"instanceName":"1"}),"instanceName":"1"}),"instanceName":"1"}),"instanceName":"1"}),"instanceName":"1"}),"instanceName":"1"});
            var Q1769;
            Q1769=makeQuery(id+"F13.opPattern","COPY",BODY,{"derivedFrom":makeQuery(id+"F10.opPattern","COPY",BODY,{"derivedFrom":makeQuery(id+"F7.opPattern","COPY",BODY,{"derivedFrom":makeQuery(id+"F6.opPattern","COPY",BODY,{"derivedFrom":makeQuery(id+"F5.opPattern","COPY",BODY,{"derivedFrom":makeQuery(id+"F1.opRevolve","SWEPT_BODY",BODY,{"disambiguationData":[OSD([sQuery(id+"F0.wireOp",EDGE,"E1")])]}),"instanceName":"1"}),"instanceName":"1"}),"instanceName":"1"}),"instanceName":"1"}),"instanceName":"1"});
            var Q1770;
            Q1770=makeQuery(id+"F13.opPattern","COPY",BODY,{"derivedFrom":makeQuery(id+"F10.opPattern","COPY",BODY,{"derivedFrom":makeQuery(id+"F7.opPattern","COPY",BODY,{"derivedFrom":makeQuery(id+"F6.opPattern","COPY",BODY,{"derivedFrom":makeQuery(id+"F5.opPattern","COPY",BODY,{"derivedFrom":makeQuery(id+"F2.opPattern","COPY",BODY,{"derivedFrom":makeQuery(id+"F1.opRevolve","SWEPT_BODY",BODY,{"disambiguationData":[OSD([sQuery(id+"F0.wireOp",EDGE,"E1")])]}),"instanceName":"1"}),"instanceName":"1"}),"instanceName":"1"}),"instanceName":"1"}),"instanceName":"1"}),"instanceName":"1"});
            var Q1771;
            Q1771=makeQuery(id+"F13.opPattern","COPY",BODY,{"derivedFrom":makeQuery(id+"F10.opPattern","COPY",BODY,{"derivedFrom":makeQuery(id+"F7.opPattern","COPY",BODY,{"derivedFrom":makeQuery(id+"F6.opPattern","COPY",BODY,{"derivedFrom":makeQuery(id+"F5.opPattern","COPY",BODY,{"derivedFrom":makeQuery(id+"F3.opPattern","COPY",BODY,{"derivedFrom":makeQuery(id+"F2.opPattern","COPY",BODY,{"derivedFrom":makeQuery(id+"F1.opRevolve","SWEPT_BODY",BODY,{"disambiguationData":[OSD([sQuery(id+"F0.wireOp",EDGE,"E1")])]}),"instanceName":"1"}),"instanceName":"1"}),"instanceName":"1"}),"instanceName":"1"}),"instanceName":"1"}),"instanceName":"1"}),"instanceName":"1"});
            var Q1772;
            Q1772=makeQuery(id+"F13.opPattern","COPY",BODY,{"derivedFrom":makeQuery(id+"F10.opPattern","COPY",BODY,{"derivedFrom":makeQuery(id+"F7.opPattern","COPY",BODY,{"derivedFrom":makeQuery(id+"F6.opPattern","COPY",BODY,{"derivedFrom":makeQuery(id+"F5.opPattern","COPY",BODY,{"derivedFrom":makeQuery(id+"F4.opPattern","COPY",BODY,{"derivedFrom":makeQuery(id+"F1.opRevolve","SWEPT_BODY",BODY,{"disambiguationData":[OSD([sQuery(id+"F0.wireOp",EDGE,"E1")])]}),"instanceName":"1"}),"instanceName":"1"}),"instanceName":"1"}),"instanceName":"1"}),"instanceName":"1"}),"instanceName":"1"});
            var Q1773;
            Q1773=makeQuery(id+"F13.opPattern","COPY",BODY,{"derivedFrom":makeQuery(id+"F10.opPattern","COPY",BODY,{"derivedFrom":makeQuery(id+"F7.opPattern","COPY",BODY,{"derivedFrom":makeQuery(id+"F6.opPattern","COPY",BODY,{"derivedFrom":makeQuery(id+"F5.opPattern","COPY",BODY,{"derivedFrom":makeQuery(id+"F4.opPattern","COPY",BODY,{"derivedFrom":makeQuery(id+"F2.opPattern","COPY",BODY,{"derivedFrom":makeQuery(id+"F1.opRevolve","SWEPT_BODY",BODY,{"disambiguationData":[OSD([sQuery(id+"F0.wireOp",EDGE,"E1")])]}),"instanceName":"1"}),"instanceName":"1"}),"instanceName":"1"}),"instanceName":"1"}),"instanceName":"1"}),"instanceName":"1"}),"instanceName":"1"});
            var Q1774;
            Q1774=makeQuery(id+"F13.opPattern","COPY",BODY,{"derivedFrom":makeQuery(id+"F10.opPattern","COPY",BODY,{"derivedFrom":makeQuery(id+"F7.opPattern","COPY",BODY,{"derivedFrom":makeQuery(id+"F6.opPattern","COPY",BODY,{"derivedFrom":makeQuery(id+"F5.opPattern","COPY",BODY,{"derivedFrom":makeQuery(id+"F4.opPattern","COPY",BODY,{"derivedFrom":makeQuery(id+"F3.opPattern","COPY",BODY,{"derivedFrom":makeQuery(id+"F2.opPattern","COPY",BODY,{"derivedFrom":makeQuery(id+"F1.opRevolve","SWEPT_BODY",BODY,{"disambiguationData":[OSD([sQuery(id+"F0.wireOp",EDGE,"E1")])]}),"instanceName":"1"}),"instanceName":"1"}),"instanceName":"1"}),"instanceName":"1"}),"instanceName":"1"}),"instanceName":"1"}),"instanceName":"1"}),"instanceName":"1"});
            var Q1775;
            Q1775=makeQuery(id+"F13.opPattern","COPY",BODY,{"derivedFrom":makeQuery(id+"F10.opPattern","COPY",BODY,{"derivedFrom":makeQuery(id+"F8.opPattern","COPY",BODY,{"derivedFrom":makeQuery(id+"F1.opRevolve","SWEPT_BODY",BODY,{"disambiguationData":[OSD([sQuery(id+"F0.wireOp",EDGE,"E1")])]}),"instanceName":"1"}),"instanceName":"1"}),"instanceName":"1"});
            var Q1776;
            Q1776=makeQuery(id+"F13.opPattern","COPY",BODY,{"derivedFrom":makeQuery(id+"F10.opPattern","COPY",BODY,{"derivedFrom":makeQuery(id+"F8.opPattern","COPY",BODY,{"derivedFrom":makeQuery(id+"F2.opPattern","COPY",BODY,{"derivedFrom":makeQuery(id+"F1.opRevolve","SWEPT_BODY",BODY,{"disambiguationData":[OSD([sQuery(id+"F0.wireOp",EDGE,"E1")])]}),"instanceName":"1"}),"instanceName":"1"}),"instanceName":"1"}),"instanceName":"1"});
            var Q1777;
            Q1777=makeQuery(id+"F13.opPattern","COPY",BODY,{"derivedFrom":makeQuery(id+"F10.opPattern","COPY",BODY,{"derivedFrom":makeQuery(id+"F8.opPattern","COPY",BODY,{"derivedFrom":makeQuery(id+"F3.opPattern","COPY",BODY,{"derivedFrom":makeQuery(id+"F2.opPattern","COPY",BODY,{"derivedFrom":makeQuery(id+"F1.opRevolve","SWEPT_BODY",BODY,{"disambiguationData":[OSD([sQuery(id+"F0.wireOp",EDGE,"E1")])]}),"instanceName":"1"}),"instanceName":"1"}),"instanceName":"1"}),"instanceName":"1"}),"instanceName":"1"});
            var Q1778;
            Q1778=makeQuery(id+"F13.opPattern","COPY",BODY,{"derivedFrom":makeQuery(id+"F10.opPattern","COPY",BODY,{"derivedFrom":makeQuery(id+"F8.opPattern","COPY",BODY,{"derivedFrom":makeQuery(id+"F4.opPattern","COPY",BODY,{"derivedFrom":makeQuery(id+"F1.opRevolve","SWEPT_BODY",BODY,{"disambiguationData":[OSD([sQuery(id+"F0.wireOp",EDGE,"E1")])]}),"instanceName":"1"}),"instanceName":"1"}),"instanceName":"1"}),"instanceName":"1"});
            var Q1779;
            Q1779=makeQuery(id+"F13.opPattern","COPY",BODY,{"derivedFrom":makeQuery(id+"F10.opPattern","COPY",BODY,{"derivedFrom":makeQuery(id+"F8.opPattern","COPY",BODY,{"derivedFrom":makeQuery(id+"F4.opPattern","COPY",BODY,{"derivedFrom":makeQuery(id+"F2.opPattern","COPY",BODY,{"derivedFrom":makeQuery(id+"F1.opRevolve","SWEPT_BODY",BODY,{"disambiguationData":[OSD([sQuery(id+"F0.wireOp",EDGE,"E1")])]}),"instanceName":"1"}),"instanceName":"1"}),"instanceName":"1"}),"instanceName":"1"}),"instanceName":"1"});
            var Q1780;
            Q1780=makeQuery(id+"F13.opPattern","COPY",BODY,{"derivedFrom":makeQuery(id+"F10.opPattern","COPY",BODY,{"derivedFrom":makeQuery(id+"F8.opPattern","COPY",BODY,{"derivedFrom":makeQuery(id+"F4.opPattern","COPY",BODY,{"derivedFrom":makeQuery(id+"F3.opPattern","COPY",BODY,{"derivedFrom":makeQuery(id+"F2.opPattern","COPY",BODY,{"derivedFrom":makeQuery(id+"F1.opRevolve","SWEPT_BODY",BODY,{"disambiguationData":[OSD([sQuery(id+"F0.wireOp",EDGE,"E1")])]}),"instanceName":"1"}),"instanceName":"1"}),"instanceName":"1"}),"instanceName":"1"}),"instanceName":"1"}),"instanceName":"1"});
            var Q1781;
            Q1781=makeQuery(id+"F13.opPattern","COPY",BODY,{"derivedFrom":makeQuery(id+"F10.opPattern","COPY",BODY,{"derivedFrom":makeQuery(id+"F8.opPattern","COPY",BODY,{"derivedFrom":makeQuery(id+"F5.opPattern","COPY",BODY,{"derivedFrom":makeQuery(id+"F1.opRevolve","SWEPT_BODY",BODY,{"disambiguationData":[OSD([sQuery(id+"F0.wireOp",EDGE,"E1")])]}),"instanceName":"1"}),"instanceName":"1"}),"instanceName":"1"}),"instanceName":"1"});
            var Q1782;
            Q1782=makeQuery(id+"F13.opPattern","COPY",BODY,{"derivedFrom":makeQuery(id+"F10.opPattern","COPY",BODY,{"derivedFrom":makeQuery(id+"F8.opPattern","COPY",BODY,{"derivedFrom":makeQuery(id+"F5.opPattern","COPY",BODY,{"derivedFrom":makeQuery(id+"F2.opPattern","COPY",BODY,{"derivedFrom":makeQuery(id+"F1.opRevolve","SWEPT_BODY",BODY,{"disambiguationData":[OSD([sQuery(id+"F0.wireOp",EDGE,"E1")])]}),"instanceName":"1"}),"instanceName":"1"}),"instanceName":"1"}),"instanceName":"1"}),"instanceName":"1"});
            var Q1783;
            Q1783=makeQuery(id+"F13.opPattern","COPY",BODY,{"derivedFrom":makeQuery(id+"F10.opPattern","COPY",BODY,{"derivedFrom":makeQuery(id+"F8.opPattern","COPY",BODY,{"derivedFrom":makeQuery(id+"F5.opPattern","COPY",BODY,{"derivedFrom":makeQuery(id+"F3.opPattern","COPY",BODY,{"derivedFrom":makeQuery(id+"F2.opPattern","COPY",BODY,{"derivedFrom":makeQuery(id+"F1.opRevolve","SWEPT_BODY",BODY,{"disambiguationData":[OSD([sQuery(id+"F0.wireOp",EDGE,"E1")])]}),"instanceName":"1"}),"instanceName":"1"}),"instanceName":"1"}),"instanceName":"1"}),"instanceName":"1"}),"instanceName":"1"});
            var Q1784;
            Q1784=makeQuery(id+"F13.opPattern","COPY",BODY,{"derivedFrom":makeQuery(id+"F10.opPattern","COPY",BODY,{"derivedFrom":makeQuery(id+"F8.opPattern","COPY",BODY,{"derivedFrom":makeQuery(id+"F5.opPattern","COPY",BODY,{"derivedFrom":makeQuery(id+"F4.opPattern","COPY",BODY,{"derivedFrom":makeQuery(id+"F1.opRevolve","SWEPT_BODY",BODY,{"disambiguationData":[OSD([sQuery(id+"F0.wireOp",EDGE,"E1")])]}),"instanceName":"1"}),"instanceName":"1"}),"instanceName":"1"}),"instanceName":"1"}),"instanceName":"1"});
            var Q1785;
            Q1785=makeQuery(id+"F13.opPattern","COPY",BODY,{"derivedFrom":makeQuery(id+"F10.opPattern","COPY",BODY,{"derivedFrom":makeQuery(id+"F8.opPattern","COPY",BODY,{"derivedFrom":makeQuery(id+"F5.opPattern","COPY",BODY,{"derivedFrom":makeQuery(id+"F4.opPattern","COPY",BODY,{"derivedFrom":makeQuery(id+"F2.opPattern","COPY",BODY,{"derivedFrom":makeQuery(id+"F1.opRevolve","SWEPT_BODY",BODY,{"disambiguationData":[OSD([sQuery(id+"F0.wireOp",EDGE,"E1")])]}),"instanceName":"1"}),"instanceName":"1"}),"instanceName":"1"}),"instanceName":"1"}),"instanceName":"1"}),"instanceName":"1"});
            var Q1786;
            Q1786=makeQuery(id+"F13.opPattern","COPY",BODY,{"derivedFrom":makeQuery(id+"F10.opPattern","COPY",BODY,{"derivedFrom":makeQuery(id+"F8.opPattern","COPY",BODY,{"derivedFrom":makeQuery(id+"F5.opPattern","COPY",BODY,{"derivedFrom":makeQuery(id+"F4.opPattern","COPY",BODY,{"derivedFrom":makeQuery(id+"F3.opPattern","COPY",BODY,{"derivedFrom":makeQuery(id+"F2.opPattern","COPY",BODY,{"derivedFrom":makeQuery(id+"F1.opRevolve","SWEPT_BODY",BODY,{"disambiguationData":[OSD([sQuery(id+"F0.wireOp",EDGE,"E1")])]}),"instanceName":"1"}),"instanceName":"1"}),"instanceName":"1"}),"instanceName":"1"}),"instanceName":"1"}),"instanceName":"1"}),"instanceName":"1"});
            var Q1787;
            Q1787=makeQuery(id+"F13.opPattern","COPY",BODY,{"derivedFrom":makeQuery(id+"F10.opPattern","COPY",BODY,{"derivedFrom":makeQuery(id+"F8.opPattern","COPY",BODY,{"derivedFrom":makeQuery(id+"F6.opPattern","COPY",BODY,{"derivedFrom":makeQuery(id+"F1.opRevolve","SWEPT_BODY",BODY,{"disambiguationData":[OSD([sQuery(id+"F0.wireOp",EDGE,"E1")])]}),"instanceName":"1"}),"instanceName":"1"}),"instanceName":"1"}),"instanceName":"1"});
            var Q1788;
            Q1788=makeQuery(id+"F13.opPattern","COPY",BODY,{"derivedFrom":makeQuery(id+"F10.opPattern","COPY",BODY,{"derivedFrom":makeQuery(id+"F8.opPattern","COPY",BODY,{"derivedFrom":makeQuery(id+"F6.opPattern","COPY",BODY,{"derivedFrom":makeQuery(id+"F2.opPattern","COPY",BODY,{"derivedFrom":makeQuery(id+"F1.opRevolve","SWEPT_BODY",BODY,{"disambiguationData":[OSD([sQuery(id+"F0.wireOp",EDGE,"E1")])]}),"instanceName":"1"}),"instanceName":"1"}),"instanceName":"1"}),"instanceName":"1"}),"instanceName":"1"});
            var Q1789;
            Q1789=makeQuery(id+"F13.opPattern","COPY",BODY,{"derivedFrom":makeQuery(id+"F10.opPattern","COPY",BODY,{"derivedFrom":makeQuery(id+"F8.opPattern","COPY",BODY,{"derivedFrom":makeQuery(id+"F6.opPattern","COPY",BODY,{"derivedFrom":makeQuery(id+"F3.opPattern","COPY",BODY,{"derivedFrom":makeQuery(id+"F2.opPattern","COPY",BODY,{"derivedFrom":makeQuery(id+"F1.opRevolve","SWEPT_BODY",BODY,{"disambiguationData":[OSD([sQuery(id+"F0.wireOp",EDGE,"E1")])]}),"instanceName":"1"}),"instanceName":"1"}),"instanceName":"1"}),"instanceName":"1"}),"instanceName":"1"}),"instanceName":"1"});
            var Q1790;
            Q1790=makeQuery(id+"F13.opPattern","COPY",BODY,{"derivedFrom":makeQuery(id+"F10.opPattern","COPY",BODY,{"derivedFrom":makeQuery(id+"F8.opPattern","COPY",BODY,{"derivedFrom":makeQuery(id+"F6.opPattern","COPY",BODY,{"derivedFrom":makeQuery(id+"F4.opPattern","COPY",BODY,{"derivedFrom":makeQuery(id+"F1.opRevolve","SWEPT_BODY",BODY,{"disambiguationData":[OSD([sQuery(id+"F0.wireOp",EDGE,"E1")])]}),"instanceName":"1"}),"instanceName":"1"}),"instanceName":"1"}),"instanceName":"1"}),"instanceName":"1"});
            var Q1791;
            Q1791=makeQuery(id+"F13.opPattern","COPY",BODY,{"derivedFrom":makeQuery(id+"F10.opPattern","COPY",BODY,{"derivedFrom":makeQuery(id+"F8.opPattern","COPY",BODY,{"derivedFrom":makeQuery(id+"F6.opPattern","COPY",BODY,{"derivedFrom":makeQuery(id+"F4.opPattern","COPY",BODY,{"derivedFrom":makeQuery(id+"F2.opPattern","COPY",BODY,{"derivedFrom":makeQuery(id+"F1.opRevolve","SWEPT_BODY",BODY,{"disambiguationData":[OSD([sQuery(id+"F0.wireOp",EDGE,"E1")])]}),"instanceName":"1"}),"instanceName":"1"}),"instanceName":"1"}),"instanceName":"1"}),"instanceName":"1"}),"instanceName":"1"});
            var Q1792;
            Q1792=makeQuery(id+"F13.opPattern","COPY",BODY,{"derivedFrom":makeQuery(id+"F10.opPattern","COPY",BODY,{"derivedFrom":makeQuery(id+"F8.opPattern","COPY",BODY,{"derivedFrom":makeQuery(id+"F6.opPattern","COPY",BODY,{"derivedFrom":makeQuery(id+"F4.opPattern","COPY",BODY,{"derivedFrom":makeQuery(id+"F3.opPattern","COPY",BODY,{"derivedFrom":makeQuery(id+"F2.opPattern","COPY",BODY,{"derivedFrom":makeQuery(id+"F1.opRevolve","SWEPT_BODY",BODY,{"disambiguationData":[OSD([sQuery(id+"F0.wireOp",EDGE,"E1")])]}),"instanceName":"1"}),"instanceName":"1"}),"instanceName":"1"}),"instanceName":"1"}),"instanceName":"1"}),"instanceName":"1"}),"instanceName":"1"});
            var Q1793;
            Q1793=makeQuery(id+"F13.opPattern","COPY",BODY,{"derivedFrom":makeQuery(id+"F10.opPattern","COPY",BODY,{"derivedFrom":makeQuery(id+"F8.opPattern","COPY",BODY,{"derivedFrom":makeQuery(id+"F6.opPattern","COPY",BODY,{"derivedFrom":makeQuery(id+"F5.opPattern","COPY",BODY,{"derivedFrom":makeQuery(id+"F1.opRevolve","SWEPT_BODY",BODY,{"disambiguationData":[OSD([sQuery(id+"F0.wireOp",EDGE,"E1")])]}),"instanceName":"1"}),"instanceName":"1"}),"instanceName":"1"}),"instanceName":"1"}),"instanceName":"1"});
            var Q1794;
            Q1794=makeQuery(id+"F13.opPattern","COPY",BODY,{"derivedFrom":makeQuery(id+"F10.opPattern","COPY",BODY,{"derivedFrom":makeQuery(id+"F8.opPattern","COPY",BODY,{"derivedFrom":makeQuery(id+"F6.opPattern","COPY",BODY,{"derivedFrom":makeQuery(id+"F5.opPattern","COPY",BODY,{"derivedFrom":makeQuery(id+"F2.opPattern","COPY",BODY,{"derivedFrom":makeQuery(id+"F1.opRevolve","SWEPT_BODY",BODY,{"disambiguationData":[OSD([sQuery(id+"F0.wireOp",EDGE,"E1")])]}),"instanceName":"1"}),"instanceName":"1"}),"instanceName":"1"}),"instanceName":"1"}),"instanceName":"1"}),"instanceName":"1"});
            var Q1795;
            Q1795=makeQuery(id+"F13.opPattern","COPY",BODY,{"derivedFrom":makeQuery(id+"F10.opPattern","COPY",BODY,{"derivedFrom":makeQuery(id+"F8.opPattern","COPY",BODY,{"derivedFrom":makeQuery(id+"F6.opPattern","COPY",BODY,{"derivedFrom":makeQuery(id+"F5.opPattern","COPY",BODY,{"derivedFrom":makeQuery(id+"F3.opPattern","COPY",BODY,{"derivedFrom":makeQuery(id+"F2.opPattern","COPY",BODY,{"derivedFrom":makeQuery(id+"F1.opRevolve","SWEPT_BODY",BODY,{"disambiguationData":[OSD([sQuery(id+"F0.wireOp",EDGE,"E1")])]}),"instanceName":"1"}),"instanceName":"1"}),"instanceName":"1"}),"instanceName":"1"}),"instanceName":"1"}),"instanceName":"1"}),"instanceName":"1"});
            var Q1796;
            Q1796=makeQuery(id+"F13.opPattern","COPY",BODY,{"derivedFrom":makeQuery(id+"F10.opPattern","COPY",BODY,{"derivedFrom":makeQuery(id+"F8.opPattern","COPY",BODY,{"derivedFrom":makeQuery(id+"F6.opPattern","COPY",BODY,{"derivedFrom":makeQuery(id+"F5.opPattern","COPY",BODY,{"derivedFrom":makeQuery(id+"F4.opPattern","COPY",BODY,{"derivedFrom":makeQuery(id+"F1.opRevolve","SWEPT_BODY",BODY,{"disambiguationData":[OSD([sQuery(id+"F0.wireOp",EDGE,"E1")])]}),"instanceName":"1"}),"instanceName":"1"}),"instanceName":"1"}),"instanceName":"1"}),"instanceName":"1"}),"instanceName":"1"});
            var Q1797;
            Q1797=makeQuery(id+"F13.opPattern","COPY",BODY,{"derivedFrom":makeQuery(id+"F10.opPattern","COPY",BODY,{"derivedFrom":makeQuery(id+"F8.opPattern","COPY",BODY,{"derivedFrom":makeQuery(id+"F6.opPattern","COPY",BODY,{"derivedFrom":makeQuery(id+"F5.opPattern","COPY",BODY,{"derivedFrom":makeQuery(id+"F4.opPattern","COPY",BODY,{"derivedFrom":makeQuery(id+"F2.opPattern","COPY",BODY,{"derivedFrom":makeQuery(id+"F1.opRevolve","SWEPT_BODY",BODY,{"disambiguationData":[OSD([sQuery(id+"F0.wireOp",EDGE,"E1")])]}),"instanceName":"1"}),"instanceName":"1"}),"instanceName":"1"}),"instanceName":"1"}),"instanceName":"1"}),"instanceName":"1"}),"instanceName":"1"});
            var Q1798;
            Q1798=makeQuery(id+"F13.opPattern","COPY",BODY,{"derivedFrom":makeQuery(id+"F10.opPattern","COPY",BODY,{"derivedFrom":makeQuery(id+"F8.opPattern","COPY",BODY,{"derivedFrom":makeQuery(id+"F6.opPattern","COPY",BODY,{"derivedFrom":makeQuery(id+"F5.opPattern","COPY",BODY,{"derivedFrom":makeQuery(id+"F4.opPattern","COPY",BODY,{"derivedFrom":makeQuery(id+"F3.opPattern","COPY",BODY,{"derivedFrom":makeQuery(id+"F2.opPattern","COPY",BODY,{"derivedFrom":makeQuery(id+"F1.opRevolve","SWEPT_BODY",BODY,{"disambiguationData":[OSD([sQuery(id+"F0.wireOp",EDGE,"E1")])]}),"instanceName":"1"}),"instanceName":"1"}),"instanceName":"1"}),"instanceName":"1"}),"instanceName":"1"}),"instanceName":"1"}),"instanceName":"1"}),"instanceName":"1"});
            var Q1799;
            Q1799=makeQuery(id+"F13.opPattern","COPY",BODY,{"derivedFrom":makeQuery(id+"F10.opPattern","COPY",BODY,{"derivedFrom":makeQuery(id+"F8.opPattern","COPY",BODY,{"derivedFrom":makeQuery(id+"F7.opPattern","COPY",BODY,{"derivedFrom":makeQuery(id+"F1.opRevolve","SWEPT_BODY",BODY,{"disambiguationData":[OSD([sQuery(id+"F0.wireOp",EDGE,"E1")])]}),"instanceName":"1"}),"instanceName":"1"}),"instanceName":"1"}),"instanceName":"1"});
            var Q1800;
            Q1800=makeQuery(id+"F13.opPattern","COPY",BODY,{"derivedFrom":makeQuery(id+"F10.opPattern","COPY",BODY,{"derivedFrom":makeQuery(id+"F8.opPattern","COPY",BODY,{"derivedFrom":makeQuery(id+"F7.opPattern","COPY",BODY,{"derivedFrom":makeQuery(id+"F2.opPattern","COPY",BODY,{"derivedFrom":makeQuery(id+"F1.opRevolve","SWEPT_BODY",BODY,{"disambiguationData":[OSD([sQuery(id+"F0.wireOp",EDGE,"E1")])]}),"instanceName":"1"}),"instanceName":"1"}),"instanceName":"1"}),"instanceName":"1"}),"instanceName":"1"});
            var Q1801;
            Q1801=makeQuery(id+"F13.opPattern","COPY",BODY,{"derivedFrom":makeQuery(id+"F10.opPattern","COPY",BODY,{"derivedFrom":makeQuery(id+"F8.opPattern","COPY",BODY,{"derivedFrom":makeQuery(id+"F7.opPattern","COPY",BODY,{"derivedFrom":makeQuery(id+"F3.opPattern","COPY",BODY,{"derivedFrom":makeQuery(id+"F2.opPattern","COPY",BODY,{"derivedFrom":makeQuery(id+"F1.opRevolve","SWEPT_BODY",BODY,{"disambiguationData":[OSD([sQuery(id+"F0.wireOp",EDGE,"E1")])]}),"instanceName":"1"}),"instanceName":"1"}),"instanceName":"1"}),"instanceName":"1"}),"instanceName":"1"}),"instanceName":"1"});
            var Q1802;
            Q1802=makeQuery(id+"F13.opPattern","COPY",BODY,{"derivedFrom":makeQuery(id+"F10.opPattern","COPY",BODY,{"derivedFrom":makeQuery(id+"F8.opPattern","COPY",BODY,{"derivedFrom":makeQuery(id+"F7.opPattern","COPY",BODY,{"derivedFrom":makeQuery(id+"F4.opPattern","COPY",BODY,{"derivedFrom":makeQuery(id+"F1.opRevolve","SWEPT_BODY",BODY,{"disambiguationData":[OSD([sQuery(id+"F0.wireOp",EDGE,"E1")])]}),"instanceName":"1"}),"instanceName":"1"}),"instanceName":"1"}),"instanceName":"1"}),"instanceName":"1"});
            var Q1803;
            Q1803=makeQuery(id+"F13.opPattern","COPY",BODY,{"derivedFrom":makeQuery(id+"F10.opPattern","COPY",BODY,{"derivedFrom":makeQuery(id+"F8.opPattern","COPY",BODY,{"derivedFrom":makeQuery(id+"F7.opPattern","COPY",BODY,{"derivedFrom":makeQuery(id+"F4.opPattern","COPY",BODY,{"derivedFrom":makeQuery(id+"F2.opPattern","COPY",BODY,{"derivedFrom":makeQuery(id+"F1.opRevolve","SWEPT_BODY",BODY,{"disambiguationData":[OSD([sQuery(id+"F0.wireOp",EDGE,"E1")])]}),"instanceName":"1"}),"instanceName":"1"}),"instanceName":"1"}),"instanceName":"1"}),"instanceName":"1"}),"instanceName":"1"});
            var Q1804;
            Q1804=makeQuery(id+"F13.opPattern","COPY",BODY,{"derivedFrom":makeQuery(id+"F10.opPattern","COPY",BODY,{"derivedFrom":makeQuery(id+"F8.opPattern","COPY",BODY,{"derivedFrom":makeQuery(id+"F7.opPattern","COPY",BODY,{"derivedFrom":makeQuery(id+"F4.opPattern","COPY",BODY,{"derivedFrom":makeQuery(id+"F3.opPattern","COPY",BODY,{"derivedFrom":makeQuery(id+"F2.opPattern","COPY",BODY,{"derivedFrom":makeQuery(id+"F1.opRevolve","SWEPT_BODY",BODY,{"disambiguationData":[OSD([sQuery(id+"F0.wireOp",EDGE,"E1")])]}),"instanceName":"1"}),"instanceName":"1"}),"instanceName":"1"}),"instanceName":"1"}),"instanceName":"1"}),"instanceName":"1"}),"instanceName":"1"});
            var Q1805;
            Q1805=makeQuery(id+"F13.opPattern","COPY",BODY,{"derivedFrom":makeQuery(id+"F10.opPattern","COPY",BODY,{"derivedFrom":makeQuery(id+"F8.opPattern","COPY",BODY,{"derivedFrom":makeQuery(id+"F7.opPattern","COPY",BODY,{"derivedFrom":makeQuery(id+"F5.opPattern","COPY",BODY,{"derivedFrom":makeQuery(id+"F1.opRevolve","SWEPT_BODY",BODY,{"disambiguationData":[OSD([sQuery(id+"F0.wireOp",EDGE,"E1")])]}),"instanceName":"1"}),"instanceName":"1"}),"instanceName":"1"}),"instanceName":"1"}),"instanceName":"1"});
            var Q1806;
            Q1806=makeQuery(id+"F13.opPattern","COPY",BODY,{"derivedFrom":makeQuery(id+"F10.opPattern","COPY",BODY,{"derivedFrom":makeQuery(id+"F8.opPattern","COPY",BODY,{"derivedFrom":makeQuery(id+"F7.opPattern","COPY",BODY,{"derivedFrom":makeQuery(id+"F5.opPattern","COPY",BODY,{"derivedFrom":makeQuery(id+"F2.opPattern","COPY",BODY,{"derivedFrom":makeQuery(id+"F1.opRevolve","SWEPT_BODY",BODY,{"disambiguationData":[OSD([sQuery(id+"F0.wireOp",EDGE,"E1")])]}),"instanceName":"1"}),"instanceName":"1"}),"instanceName":"1"}),"instanceName":"1"}),"instanceName":"1"}),"instanceName":"1"});
            var Q1807;
            Q1807=makeQuery(id+"F13.opPattern","COPY",BODY,{"derivedFrom":makeQuery(id+"F10.opPattern","COPY",BODY,{"derivedFrom":makeQuery(id+"F8.opPattern","COPY",BODY,{"derivedFrom":makeQuery(id+"F7.opPattern","COPY",BODY,{"derivedFrom":makeQuery(id+"F5.opPattern","COPY",BODY,{"derivedFrom":makeQuery(id+"F3.opPattern","COPY",BODY,{"derivedFrom":makeQuery(id+"F2.opPattern","COPY",BODY,{"derivedFrom":makeQuery(id+"F1.opRevolve","SWEPT_BODY",BODY,{"disambiguationData":[OSD([sQuery(id+"F0.wireOp",EDGE,"E1")])]}),"instanceName":"1"}),"instanceName":"1"}),"instanceName":"1"}),"instanceName":"1"}),"instanceName":"1"}),"instanceName":"1"}),"instanceName":"1"});
            var Q1808;
            Q1808=makeQuery(id+"F13.opPattern","COPY",BODY,{"derivedFrom":makeQuery(id+"F10.opPattern","COPY",BODY,{"derivedFrom":makeQuery(id+"F8.opPattern","COPY",BODY,{"derivedFrom":makeQuery(id+"F7.opPattern","COPY",BODY,{"derivedFrom":makeQuery(id+"F5.opPattern","COPY",BODY,{"derivedFrom":makeQuery(id+"F4.opPattern","COPY",BODY,{"derivedFrom":makeQuery(id+"F1.opRevolve","SWEPT_BODY",BODY,{"disambiguationData":[OSD([sQuery(id+"F0.wireOp",EDGE,"E1")])]}),"instanceName":"1"}),"instanceName":"1"}),"instanceName":"1"}),"instanceName":"1"}),"instanceName":"1"}),"instanceName":"1"});
            var Q1809;
            Q1809=makeQuery(id+"F13.opPattern","COPY",BODY,{"derivedFrom":makeQuery(id+"F10.opPattern","COPY",BODY,{"derivedFrom":makeQuery(id+"F8.opPattern","COPY",BODY,{"derivedFrom":makeQuery(id+"F7.opPattern","COPY",BODY,{"derivedFrom":makeQuery(id+"F5.opPattern","COPY",BODY,{"derivedFrom":makeQuery(id+"F4.opPattern","COPY",BODY,{"derivedFrom":makeQuery(id+"F2.opPattern","COPY",BODY,{"derivedFrom":makeQuery(id+"F1.opRevolve","SWEPT_BODY",BODY,{"disambiguationData":[OSD([sQuery(id+"F0.wireOp",EDGE,"E1")])]}),"instanceName":"1"}),"instanceName":"1"}),"instanceName":"1"}),"instanceName":"1"}),"instanceName":"1"}),"instanceName":"1"}),"instanceName":"1"});
            var Q1810;
            Q1810=makeQuery(id+"F13.opPattern","COPY",BODY,{"derivedFrom":makeQuery(id+"F10.opPattern","COPY",BODY,{"derivedFrom":makeQuery(id+"F8.opPattern","COPY",BODY,{"derivedFrom":makeQuery(id+"F7.opPattern","COPY",BODY,{"derivedFrom":makeQuery(id+"F5.opPattern","COPY",BODY,{"derivedFrom":makeQuery(id+"F4.opPattern","COPY",BODY,{"derivedFrom":makeQuery(id+"F3.opPattern","COPY",BODY,{"derivedFrom":makeQuery(id+"F2.opPattern","COPY",BODY,{"derivedFrom":makeQuery(id+"F1.opRevolve","SWEPT_BODY",BODY,{"disambiguationData":[OSD([sQuery(id+"F0.wireOp",EDGE,"E1")])]}),"instanceName":"1"}),"instanceName":"1"}),"instanceName":"1"}),"instanceName":"1"}),"instanceName":"1"}),"instanceName":"1"}),"instanceName":"1"}),"instanceName":"1"});
            var Q1811;
            Q1811=makeQuery(id+"F13.opPattern","COPY",BODY,{"derivedFrom":makeQuery(id+"F10.opPattern","COPY",BODY,{"derivedFrom":makeQuery(id+"F8.opPattern","COPY",BODY,{"derivedFrom":makeQuery(id+"F7.opPattern","COPY",BODY,{"derivedFrom":makeQuery(id+"F6.opPattern","COPY",BODY,{"derivedFrom":makeQuery(id+"F1.opRevolve","SWEPT_BODY",BODY,{"disambiguationData":[OSD([sQuery(id+"F0.wireOp",EDGE,"E1")])]}),"instanceName":"1"}),"instanceName":"1"}),"instanceName":"1"}),"instanceName":"1"}),"instanceName":"1"});
            var Q1812;
            Q1812=makeQuery(id+"F13.opPattern","COPY",BODY,{"derivedFrom":makeQuery(id+"F10.opPattern","COPY",BODY,{"derivedFrom":makeQuery(id+"F8.opPattern","COPY",BODY,{"derivedFrom":makeQuery(id+"F7.opPattern","COPY",BODY,{"derivedFrom":makeQuery(id+"F6.opPattern","COPY",BODY,{"derivedFrom":makeQuery(id+"F2.opPattern","COPY",BODY,{"derivedFrom":makeQuery(id+"F1.opRevolve","SWEPT_BODY",BODY,{"disambiguationData":[OSD([sQuery(id+"F0.wireOp",EDGE,"E1")])]}),"instanceName":"1"}),"instanceName":"1"}),"instanceName":"1"}),"instanceName":"1"}),"instanceName":"1"}),"instanceName":"1"});
            var Q1813;
            Q1813=makeQuery(id+"F13.opPattern","COPY",BODY,{"derivedFrom":makeQuery(id+"F10.opPattern","COPY",BODY,{"derivedFrom":makeQuery(id+"F8.opPattern","COPY",BODY,{"derivedFrom":makeQuery(id+"F7.opPattern","COPY",BODY,{"derivedFrom":makeQuery(id+"F6.opPattern","COPY",BODY,{"derivedFrom":makeQuery(id+"F3.opPattern","COPY",BODY,{"derivedFrom":makeQuery(id+"F2.opPattern","COPY",BODY,{"derivedFrom":makeQuery(id+"F1.opRevolve","SWEPT_BODY",BODY,{"disambiguationData":[OSD([sQuery(id+"F0.wireOp",EDGE,"E1")])]}),"instanceName":"1"}),"instanceName":"1"}),"instanceName":"1"}),"instanceName":"1"}),"instanceName":"1"}),"instanceName":"1"}),"instanceName":"1"});
            var Q1814;
            Q1814=makeQuery(id+"F13.opPattern","COPY",BODY,{"derivedFrom":makeQuery(id+"F10.opPattern","COPY",BODY,{"derivedFrom":makeQuery(id+"F8.opPattern","COPY",BODY,{"derivedFrom":makeQuery(id+"F7.opPattern","COPY",BODY,{"derivedFrom":makeQuery(id+"F6.opPattern","COPY",BODY,{"derivedFrom":makeQuery(id+"F4.opPattern","COPY",BODY,{"derivedFrom":makeQuery(id+"F1.opRevolve","SWEPT_BODY",BODY,{"disambiguationData":[OSD([sQuery(id+"F0.wireOp",EDGE,"E1")])]}),"instanceName":"1"}),"instanceName":"1"}),"instanceName":"1"}),"instanceName":"1"}),"instanceName":"1"}),"instanceName":"1"});
            var Q1815;
            Q1815=makeQuery(id+"F13.opPattern","COPY",BODY,{"derivedFrom":makeQuery(id+"F10.opPattern","COPY",BODY,{"derivedFrom":makeQuery(id+"F8.opPattern","COPY",BODY,{"derivedFrom":makeQuery(id+"F7.opPattern","COPY",BODY,{"derivedFrom":makeQuery(id+"F6.opPattern","COPY",BODY,{"derivedFrom":makeQuery(id+"F4.opPattern","COPY",BODY,{"derivedFrom":makeQuery(id+"F2.opPattern","COPY",BODY,{"derivedFrom":makeQuery(id+"F1.opRevolve","SWEPT_BODY",BODY,{"disambiguationData":[OSD([sQuery(id+"F0.wireOp",EDGE,"E1")])]}),"instanceName":"1"}),"instanceName":"1"}),"instanceName":"1"}),"instanceName":"1"}),"instanceName":"1"}),"instanceName":"1"}),"instanceName":"1"});
            var Q1816;
            Q1816=makeQuery(id+"F13.opPattern","COPY",BODY,{"derivedFrom":makeQuery(id+"F10.opPattern","COPY",BODY,{"derivedFrom":makeQuery(id+"F8.opPattern","COPY",BODY,{"derivedFrom":makeQuery(id+"F7.opPattern","COPY",BODY,{"derivedFrom":makeQuery(id+"F6.opPattern","COPY",BODY,{"derivedFrom":makeQuery(id+"F4.opPattern","COPY",BODY,{"derivedFrom":makeQuery(id+"F3.opPattern","COPY",BODY,{"derivedFrom":makeQuery(id+"F2.opPattern","COPY",BODY,{"derivedFrom":makeQuery(id+"F1.opRevolve","SWEPT_BODY",BODY,{"disambiguationData":[OSD([sQuery(id+"F0.wireOp",EDGE,"E1")])]}),"instanceName":"1"}),"instanceName":"1"}),"instanceName":"1"}),"instanceName":"1"}),"instanceName":"1"}),"instanceName":"1"}),"instanceName":"1"}),"instanceName":"1"});
            var Q1817;
            Q1817=makeQuery(id+"F13.opPattern","COPY",BODY,{"derivedFrom":makeQuery(id+"F10.opPattern","COPY",BODY,{"derivedFrom":makeQuery(id+"F8.opPattern","COPY",BODY,{"derivedFrom":makeQuery(id+"F7.opPattern","COPY",BODY,{"derivedFrom":makeQuery(id+"F6.opPattern","COPY",BODY,{"derivedFrom":makeQuery(id+"F5.opPattern","COPY",BODY,{"derivedFrom":makeQuery(id+"F1.opRevolve","SWEPT_BODY",BODY,{"disambiguationData":[OSD([sQuery(id+"F0.wireOp",EDGE,"E1")])]}),"instanceName":"1"}),"instanceName":"1"}),"instanceName":"1"}),"instanceName":"1"}),"instanceName":"1"}),"instanceName":"1"});
            var Q1818;
            Q1818=makeQuery(id+"F13.opPattern","COPY",BODY,{"derivedFrom":makeQuery(id+"F10.opPattern","COPY",BODY,{"derivedFrom":makeQuery(id+"F8.opPattern","COPY",BODY,{"derivedFrom":makeQuery(id+"F7.opPattern","COPY",BODY,{"derivedFrom":makeQuery(id+"F6.opPattern","COPY",BODY,{"derivedFrom":makeQuery(id+"F5.opPattern","COPY",BODY,{"derivedFrom":makeQuery(id+"F2.opPattern","COPY",BODY,{"derivedFrom":makeQuery(id+"F1.opRevolve","SWEPT_BODY",BODY,{"disambiguationData":[OSD([sQuery(id+"F0.wireOp",EDGE,"E1")])]}),"instanceName":"1"}),"instanceName":"1"}),"instanceName":"1"}),"instanceName":"1"}),"instanceName":"1"}),"instanceName":"1"}),"instanceName":"1"});
            var Q1819;
            Q1819=makeQuery(id+"F13.opPattern","COPY",BODY,{"derivedFrom":makeQuery(id+"F10.opPattern","COPY",BODY,{"derivedFrom":makeQuery(id+"F8.opPattern","COPY",BODY,{"derivedFrom":makeQuery(id+"F7.opPattern","COPY",BODY,{"derivedFrom":makeQuery(id+"F6.opPattern","COPY",BODY,{"derivedFrom":makeQuery(id+"F5.opPattern","COPY",BODY,{"derivedFrom":makeQuery(id+"F3.opPattern","COPY",BODY,{"derivedFrom":makeQuery(id+"F2.opPattern","COPY",BODY,{"derivedFrom":makeQuery(id+"F1.opRevolve","SWEPT_BODY",BODY,{"disambiguationData":[OSD([sQuery(id+"F0.wireOp",EDGE,"E1")])]}),"instanceName":"1"}),"instanceName":"1"}),"instanceName":"1"}),"instanceName":"1"}),"instanceName":"1"}),"instanceName":"1"}),"instanceName":"1"}),"instanceName":"1"});
            var Q1820;
            Q1820=makeQuery(id+"F13.opPattern","COPY",BODY,{"derivedFrom":makeQuery(id+"F10.opPattern","COPY",BODY,{"derivedFrom":makeQuery(id+"F8.opPattern","COPY",BODY,{"derivedFrom":makeQuery(id+"F7.opPattern","COPY",BODY,{"derivedFrom":makeQuery(id+"F6.opPattern","COPY",BODY,{"derivedFrom":makeQuery(id+"F5.opPattern","COPY",BODY,{"derivedFrom":makeQuery(id+"F4.opPattern","COPY",BODY,{"derivedFrom":makeQuery(id+"F1.opRevolve","SWEPT_BODY",BODY,{"disambiguationData":[OSD([sQuery(id+"F0.wireOp",EDGE,"E1")])]}),"instanceName":"1"}),"instanceName":"1"}),"instanceName":"1"}),"instanceName":"1"}),"instanceName":"1"}),"instanceName":"1"}),"instanceName":"1"});
            var Q1821;
            Q1821=makeQuery(id+"F13.opPattern","COPY",BODY,{"derivedFrom":makeQuery(id+"F10.opPattern","COPY",BODY,{"derivedFrom":makeQuery(id+"F8.opPattern","COPY",BODY,{"derivedFrom":makeQuery(id+"F7.opPattern","COPY",BODY,{"derivedFrom":makeQuery(id+"F6.opPattern","COPY",BODY,{"derivedFrom":makeQuery(id+"F5.opPattern","COPY",BODY,{"derivedFrom":makeQuery(id+"F4.opPattern","COPY",BODY,{"derivedFrom":makeQuery(id+"F2.opPattern","COPY",BODY,{"derivedFrom":makeQuery(id+"F1.opRevolve","SWEPT_BODY",BODY,{"disambiguationData":[OSD([sQuery(id+"F0.wireOp",EDGE,"E1")])]}),"instanceName":"1"}),"instanceName":"1"}),"instanceName":"1"}),"instanceName":"1"}),"instanceName":"1"}),"instanceName":"1"}),"instanceName":"1"}),"instanceName":"1"});
            var Q1822;
            Q1822=makeQuery(id+"F13.opPattern","COPY",BODY,{"derivedFrom":makeQuery(id+"F10.opPattern","COPY",BODY,{"derivedFrom":makeQuery(id+"F8.opPattern","COPY",BODY,{"derivedFrom":makeQuery(id+"F7.opPattern","COPY",BODY,{"derivedFrom":makeQuery(id+"F6.opPattern","COPY",BODY,{"derivedFrom":makeQuery(id+"F5.opPattern","COPY",BODY,{"derivedFrom":makeQuery(id+"F4.opPattern","COPY",BODY,{"derivedFrom":makeQuery(id+"F3.opPattern","COPY",BODY,{"derivedFrom":makeQuery(id+"F2.opPattern","COPY",BODY,{"derivedFrom":makeQuery(id+"F1.opRevolve","SWEPT_BODY",BODY,{"disambiguationData":[OSD([sQuery(id+"F0.wireOp",EDGE,"E1")])]}),"instanceName":"1"}),"instanceName":"1"}),"instanceName":"1"}),"instanceName":"1"}),"instanceName":"1"}),"instanceName":"1"}),"instanceName":"1"}),"instanceName":"1"}),"instanceName":"1"});
            var Q1823;
            Q1823=makeQuery(id+"F13.opPattern","COPY",BODY,{"derivedFrom":makeQuery(id+"F10.opPattern","COPY",BODY,{"derivedFrom":makeQuery(id+"F9.opPattern","COPY",BODY,{"derivedFrom":makeQuery(id+"F1.opRevolve","SWEPT_BODY",BODY,{"disambiguationData":[OSD([sQuery(id+"F0.wireOp",EDGE,"E1")])]}),"instanceName":"1"}),"instanceName":"1"}),"instanceName":"1"});
            var Q1824;
            Q1824=makeQuery(id+"F13.opPattern","COPY",BODY,{"derivedFrom":makeQuery(id+"F10.opPattern","COPY",BODY,{"derivedFrom":makeQuery(id+"F9.opPattern","COPY",BODY,{"derivedFrom":makeQuery(id+"F2.opPattern","COPY",BODY,{"derivedFrom":makeQuery(id+"F1.opRevolve","SWEPT_BODY",BODY,{"disambiguationData":[OSD([sQuery(id+"F0.wireOp",EDGE,"E1")])]}),"instanceName":"1"}),"instanceName":"1"}),"instanceName":"1"}),"instanceName":"1"});
            var Q1825;
            Q1825=makeQuery(id+"F13.opPattern","COPY",BODY,{"derivedFrom":makeQuery(id+"F10.opPattern","COPY",BODY,{"derivedFrom":makeQuery(id+"F9.opPattern","COPY",BODY,{"derivedFrom":makeQuery(id+"F3.opPattern","COPY",BODY,{"derivedFrom":makeQuery(id+"F2.opPattern","COPY",BODY,{"derivedFrom":makeQuery(id+"F1.opRevolve","SWEPT_BODY",BODY,{"disambiguationData":[OSD([sQuery(id+"F0.wireOp",EDGE,"E1")])]}),"instanceName":"1"}),"instanceName":"1"}),"instanceName":"1"}),"instanceName":"1"}),"instanceName":"1"});
            var Q1826;
            Q1826=makeQuery(id+"F13.opPattern","COPY",BODY,{"derivedFrom":makeQuery(id+"F10.opPattern","COPY",BODY,{"derivedFrom":makeQuery(id+"F9.opPattern","COPY",BODY,{"derivedFrom":makeQuery(id+"F4.opPattern","COPY",BODY,{"derivedFrom":makeQuery(id+"F1.opRevolve","SWEPT_BODY",BODY,{"disambiguationData":[OSD([sQuery(id+"F0.wireOp",EDGE,"E1")])]}),"instanceName":"1"}),"instanceName":"1"}),"instanceName":"1"}),"instanceName":"1"});
            var Q1827;
            Q1827=makeQuery(id+"F13.opPattern","COPY",BODY,{"derivedFrom":makeQuery(id+"F10.opPattern","COPY",BODY,{"derivedFrom":makeQuery(id+"F9.opPattern","COPY",BODY,{"derivedFrom":makeQuery(id+"F4.opPattern","COPY",BODY,{"derivedFrom":makeQuery(id+"F2.opPattern","COPY",BODY,{"derivedFrom":makeQuery(id+"F1.opRevolve","SWEPT_BODY",BODY,{"disambiguationData":[OSD([sQuery(id+"F0.wireOp",EDGE,"E1")])]}),"instanceName":"1"}),"instanceName":"1"}),"instanceName":"1"}),"instanceName":"1"}),"instanceName":"1"});
            var Q1828;
            Q1828=makeQuery(id+"F13.opPattern","COPY",BODY,{"derivedFrom":makeQuery(id+"F10.opPattern","COPY",BODY,{"derivedFrom":makeQuery(id+"F9.opPattern","COPY",BODY,{"derivedFrom":makeQuery(id+"F4.opPattern","COPY",BODY,{"derivedFrom":makeQuery(id+"F3.opPattern","COPY",BODY,{"derivedFrom":makeQuery(id+"F2.opPattern","COPY",BODY,{"derivedFrom":makeQuery(id+"F1.opRevolve","SWEPT_BODY",BODY,{"disambiguationData":[OSD([sQuery(id+"F0.wireOp",EDGE,"E1")])]}),"instanceName":"1"}),"instanceName":"1"}),"instanceName":"1"}),"instanceName":"1"}),"instanceName":"1"}),"instanceName":"1"});
            var Q1829;
            Q1829=makeQuery(id+"F13.opPattern","COPY",BODY,{"derivedFrom":makeQuery(id+"F10.opPattern","COPY",BODY,{"derivedFrom":makeQuery(id+"F9.opPattern","COPY",BODY,{"derivedFrom":makeQuery(id+"F5.opPattern","COPY",BODY,{"derivedFrom":makeQuery(id+"F1.opRevolve","SWEPT_BODY",BODY,{"disambiguationData":[OSD([sQuery(id+"F0.wireOp",EDGE,"E1")])]}),"instanceName":"1"}),"instanceName":"1"}),"instanceName":"1"}),"instanceName":"1"});
            var Q1830;
            Q1830=makeQuery(id+"F13.opPattern","COPY",BODY,{"derivedFrom":makeQuery(id+"F10.opPattern","COPY",BODY,{"derivedFrom":makeQuery(id+"F9.opPattern","COPY",BODY,{"derivedFrom":makeQuery(id+"F5.opPattern","COPY",BODY,{"derivedFrom":makeQuery(id+"F2.opPattern","COPY",BODY,{"derivedFrom":makeQuery(id+"F1.opRevolve","SWEPT_BODY",BODY,{"disambiguationData":[OSD([sQuery(id+"F0.wireOp",EDGE,"E1")])]}),"instanceName":"1"}),"instanceName":"1"}),"instanceName":"1"}),"instanceName":"1"}),"instanceName":"1"});
            var Q1831;
            Q1831=makeQuery(id+"F13.opPattern","COPY",BODY,{"derivedFrom":makeQuery(id+"F10.opPattern","COPY",BODY,{"derivedFrom":makeQuery(id+"F9.opPattern","COPY",BODY,{"derivedFrom":makeQuery(id+"F5.opPattern","COPY",BODY,{"derivedFrom":makeQuery(id+"F3.opPattern","COPY",BODY,{"derivedFrom":makeQuery(id+"F2.opPattern","COPY",BODY,{"derivedFrom":makeQuery(id+"F1.opRevolve","SWEPT_BODY",BODY,{"disambiguationData":[OSD([sQuery(id+"F0.wireOp",EDGE,"E1")])]}),"instanceName":"1"}),"instanceName":"1"}),"instanceName":"1"}),"instanceName":"1"}),"instanceName":"1"}),"instanceName":"1"});
            var Q1832;
            Q1832=makeQuery(id+"F13.opPattern","COPY",BODY,{"derivedFrom":makeQuery(id+"F10.opPattern","COPY",BODY,{"derivedFrom":makeQuery(id+"F9.opPattern","COPY",BODY,{"derivedFrom":makeQuery(id+"F5.opPattern","COPY",BODY,{"derivedFrom":makeQuery(id+"F4.opPattern","COPY",BODY,{"derivedFrom":makeQuery(id+"F1.opRevolve","SWEPT_BODY",BODY,{"disambiguationData":[OSD([sQuery(id+"F0.wireOp",EDGE,"E1")])]}),"instanceName":"1"}),"instanceName":"1"}),"instanceName":"1"}),"instanceName":"1"}),"instanceName":"1"});
            var Q1833;
            Q1833=makeQuery(id+"F13.opPattern","COPY",BODY,{"derivedFrom":makeQuery(id+"F10.opPattern","COPY",BODY,{"derivedFrom":makeQuery(id+"F9.opPattern","COPY",BODY,{"derivedFrom":makeQuery(id+"F5.opPattern","COPY",BODY,{"derivedFrom":makeQuery(id+"F4.opPattern","COPY",BODY,{"derivedFrom":makeQuery(id+"F2.opPattern","COPY",BODY,{"derivedFrom":makeQuery(id+"F1.opRevolve","SWEPT_BODY",BODY,{"disambiguationData":[OSD([sQuery(id+"F0.wireOp",EDGE,"E1")])]}),"instanceName":"1"}),"instanceName":"1"}),"instanceName":"1"}),"instanceName":"1"}),"instanceName":"1"}),"instanceName":"1"});
            var Q1834;
            Q1834=makeQuery(id+"F13.opPattern","COPY",BODY,{"derivedFrom":makeQuery(id+"F10.opPattern","COPY",BODY,{"derivedFrom":makeQuery(id+"F9.opPattern","COPY",BODY,{"derivedFrom":makeQuery(id+"F5.opPattern","COPY",BODY,{"derivedFrom":makeQuery(id+"F4.opPattern","COPY",BODY,{"derivedFrom":makeQuery(id+"F3.opPattern","COPY",BODY,{"derivedFrom":makeQuery(id+"F2.opPattern","COPY",BODY,{"derivedFrom":makeQuery(id+"F1.opRevolve","SWEPT_BODY",BODY,{"disambiguationData":[OSD([sQuery(id+"F0.wireOp",EDGE,"E1")])]}),"instanceName":"1"}),"instanceName":"1"}),"instanceName":"1"}),"instanceName":"1"}),"instanceName":"1"}),"instanceName":"1"}),"instanceName":"1"});
            var Q1835;
            Q1835=makeQuery(id+"F13.opPattern","COPY",BODY,{"derivedFrom":makeQuery(id+"F10.opPattern","COPY",BODY,{"derivedFrom":makeQuery(id+"F9.opPattern","COPY",BODY,{"derivedFrom":makeQuery(id+"F6.opPattern","COPY",BODY,{"derivedFrom":makeQuery(id+"F1.opRevolve","SWEPT_BODY",BODY,{"disambiguationData":[OSD([sQuery(id+"F0.wireOp",EDGE,"E1")])]}),"instanceName":"1"}),"instanceName":"1"}),"instanceName":"1"}),"instanceName":"1"});
            var Q1836;
            Q1836=makeQuery(id+"F13.opPattern","COPY",BODY,{"derivedFrom":makeQuery(id+"F10.opPattern","COPY",BODY,{"derivedFrom":makeQuery(id+"F9.opPattern","COPY",BODY,{"derivedFrom":makeQuery(id+"F6.opPattern","COPY",BODY,{"derivedFrom":makeQuery(id+"F2.opPattern","COPY",BODY,{"derivedFrom":makeQuery(id+"F1.opRevolve","SWEPT_BODY",BODY,{"disambiguationData":[OSD([sQuery(id+"F0.wireOp",EDGE,"E1")])]}),"instanceName":"1"}),"instanceName":"1"}),"instanceName":"1"}),"instanceName":"1"}),"instanceName":"1"});
            var Q1837;
            Q1837=makeQuery(id+"F13.opPattern","COPY",BODY,{"derivedFrom":makeQuery(id+"F10.opPattern","COPY",BODY,{"derivedFrom":makeQuery(id+"F9.opPattern","COPY",BODY,{"derivedFrom":makeQuery(id+"F6.opPattern","COPY",BODY,{"derivedFrom":makeQuery(id+"F3.opPattern","COPY",BODY,{"derivedFrom":makeQuery(id+"F2.opPattern","COPY",BODY,{"derivedFrom":makeQuery(id+"F1.opRevolve","SWEPT_BODY",BODY,{"disambiguationData":[OSD([sQuery(id+"F0.wireOp",EDGE,"E1")])]}),"instanceName":"1"}),"instanceName":"1"}),"instanceName":"1"}),"instanceName":"1"}),"instanceName":"1"}),"instanceName":"1"});
            var Q1838;
            Q1838=makeQuery(id+"F13.opPattern","COPY",BODY,{"derivedFrom":makeQuery(id+"F10.opPattern","COPY",BODY,{"derivedFrom":makeQuery(id+"F9.opPattern","COPY",BODY,{"derivedFrom":makeQuery(id+"F6.opPattern","COPY",BODY,{"derivedFrom":makeQuery(id+"F4.opPattern","COPY",BODY,{"derivedFrom":makeQuery(id+"F1.opRevolve","SWEPT_BODY",BODY,{"disambiguationData":[OSD([sQuery(id+"F0.wireOp",EDGE,"E1")])]}),"instanceName":"1"}),"instanceName":"1"}),"instanceName":"1"}),"instanceName":"1"}),"instanceName":"1"});
            var Q1839;
            Q1839=makeQuery(id+"F13.opPattern","COPY",BODY,{"derivedFrom":makeQuery(id+"F10.opPattern","COPY",BODY,{"derivedFrom":makeQuery(id+"F9.opPattern","COPY",BODY,{"derivedFrom":makeQuery(id+"F6.opPattern","COPY",BODY,{"derivedFrom":makeQuery(id+"F4.opPattern","COPY",BODY,{"derivedFrom":makeQuery(id+"F2.opPattern","COPY",BODY,{"derivedFrom":makeQuery(id+"F1.opRevolve","SWEPT_BODY",BODY,{"disambiguationData":[OSD([sQuery(id+"F0.wireOp",EDGE,"E1")])]}),"instanceName":"1"}),"instanceName":"1"}),"instanceName":"1"}),"instanceName":"1"}),"instanceName":"1"}),"instanceName":"1"});
            var Q1840;
            Q1840=makeQuery(id+"F13.opPattern","COPY",BODY,{"derivedFrom":makeQuery(id+"F10.opPattern","COPY",BODY,{"derivedFrom":makeQuery(id+"F9.opPattern","COPY",BODY,{"derivedFrom":makeQuery(id+"F6.opPattern","COPY",BODY,{"derivedFrom":makeQuery(id+"F4.opPattern","COPY",BODY,{"derivedFrom":makeQuery(id+"F3.opPattern","COPY",BODY,{"derivedFrom":makeQuery(id+"F2.opPattern","COPY",BODY,{"derivedFrom":makeQuery(id+"F1.opRevolve","SWEPT_BODY",BODY,{"disambiguationData":[OSD([sQuery(id+"F0.wireOp",EDGE,"E1")])]}),"instanceName":"1"}),"instanceName":"1"}),"instanceName":"1"}),"instanceName":"1"}),"instanceName":"1"}),"instanceName":"1"}),"instanceName":"1"});
            var Q1841;
            Q1841=makeQuery(id+"F13.opPattern","COPY",BODY,{"derivedFrom":makeQuery(id+"F10.opPattern","COPY",BODY,{"derivedFrom":makeQuery(id+"F9.opPattern","COPY",BODY,{"derivedFrom":makeQuery(id+"F6.opPattern","COPY",BODY,{"derivedFrom":makeQuery(id+"F5.opPattern","COPY",BODY,{"derivedFrom":makeQuery(id+"F1.opRevolve","SWEPT_BODY",BODY,{"disambiguationData":[OSD([sQuery(id+"F0.wireOp",EDGE,"E1")])]}),"instanceName":"1"}),"instanceName":"1"}),"instanceName":"1"}),"instanceName":"1"}),"instanceName":"1"});
            var Q1842;
            Q1842=makeQuery(id+"F13.opPattern","COPY",BODY,{"derivedFrom":makeQuery(id+"F10.opPattern","COPY",BODY,{"derivedFrom":makeQuery(id+"F9.opPattern","COPY",BODY,{"derivedFrom":makeQuery(id+"F6.opPattern","COPY",BODY,{"derivedFrom":makeQuery(id+"F5.opPattern","COPY",BODY,{"derivedFrom":makeQuery(id+"F2.opPattern","COPY",BODY,{"derivedFrom":makeQuery(id+"F1.opRevolve","SWEPT_BODY",BODY,{"disambiguationData":[OSD([sQuery(id+"F0.wireOp",EDGE,"E1")])]}),"instanceName":"1"}),"instanceName":"1"}),"instanceName":"1"}),"instanceName":"1"}),"instanceName":"1"}),"instanceName":"1"});
            var Q1843;
            Q1843=makeQuery(id+"F13.opPattern","COPY",BODY,{"derivedFrom":makeQuery(id+"F10.opPattern","COPY",BODY,{"derivedFrom":makeQuery(id+"F9.opPattern","COPY",BODY,{"derivedFrom":makeQuery(id+"F6.opPattern","COPY",BODY,{"derivedFrom":makeQuery(id+"F5.opPattern","COPY",BODY,{"derivedFrom":makeQuery(id+"F3.opPattern","COPY",BODY,{"derivedFrom":makeQuery(id+"F2.opPattern","COPY",BODY,{"derivedFrom":makeQuery(id+"F1.opRevolve","SWEPT_BODY",BODY,{"disambiguationData":[OSD([sQuery(id+"F0.wireOp",EDGE,"E1")])]}),"instanceName":"1"}),"instanceName":"1"}),"instanceName":"1"}),"instanceName":"1"}),"instanceName":"1"}),"instanceName":"1"}),"instanceName":"1"});
            var Q1844;
            Q1844=makeQuery(id+"F13.opPattern","COPY",BODY,{"derivedFrom":makeQuery(id+"F10.opPattern","COPY",BODY,{"derivedFrom":makeQuery(id+"F9.opPattern","COPY",BODY,{"derivedFrom":makeQuery(id+"F6.opPattern","COPY",BODY,{"derivedFrom":makeQuery(id+"F5.opPattern","COPY",BODY,{"derivedFrom":makeQuery(id+"F4.opPattern","COPY",BODY,{"derivedFrom":makeQuery(id+"F1.opRevolve","SWEPT_BODY",BODY,{"disambiguationData":[OSD([sQuery(id+"F0.wireOp",EDGE,"E1")])]}),"instanceName":"1"}),"instanceName":"1"}),"instanceName":"1"}),"instanceName":"1"}),"instanceName":"1"}),"instanceName":"1"});
            var Q1845;
            Q1845=makeQuery(id+"F13.opPattern","COPY",BODY,{"derivedFrom":makeQuery(id+"F10.opPattern","COPY",BODY,{"derivedFrom":makeQuery(id+"F9.opPattern","COPY",BODY,{"derivedFrom":makeQuery(id+"F6.opPattern","COPY",BODY,{"derivedFrom":makeQuery(id+"F5.opPattern","COPY",BODY,{"derivedFrom":makeQuery(id+"F4.opPattern","COPY",BODY,{"derivedFrom":makeQuery(id+"F2.opPattern","COPY",BODY,{"derivedFrom":makeQuery(id+"F1.opRevolve","SWEPT_BODY",BODY,{"disambiguationData":[OSD([sQuery(id+"F0.wireOp",EDGE,"E1")])]}),"instanceName":"1"}),"instanceName":"1"}),"instanceName":"1"}),"instanceName":"1"}),"instanceName":"1"}),"instanceName":"1"}),"instanceName":"1"});
            var Q1846;
            Q1846=makeQuery(id+"F13.opPattern","COPY",BODY,{"derivedFrom":makeQuery(id+"F10.opPattern","COPY",BODY,{"derivedFrom":makeQuery(id+"F9.opPattern","COPY",BODY,{"derivedFrom":makeQuery(id+"F6.opPattern","COPY",BODY,{"derivedFrom":makeQuery(id+"F5.opPattern","COPY",BODY,{"derivedFrom":makeQuery(id+"F4.opPattern","COPY",BODY,{"derivedFrom":makeQuery(id+"F3.opPattern","COPY",BODY,{"derivedFrom":makeQuery(id+"F2.opPattern","COPY",BODY,{"derivedFrom":makeQuery(id+"F1.opRevolve","SWEPT_BODY",BODY,{"disambiguationData":[OSD([sQuery(id+"F0.wireOp",EDGE,"E1")])]}),"instanceName":"1"}),"instanceName":"1"}),"instanceName":"1"}),"instanceName":"1"}),"instanceName":"1"}),"instanceName":"1"}),"instanceName":"1"}),"instanceName":"1"});
            var Q1847;
            Q1847=makeQuery(id+"F13.opPattern","COPY",BODY,{"derivedFrom":makeQuery(id+"F10.opPattern","COPY",BODY,{"derivedFrom":makeQuery(id+"F9.opPattern","COPY",BODY,{"derivedFrom":makeQuery(id+"F7.opPattern","COPY",BODY,{"derivedFrom":makeQuery(id+"F1.opRevolve","SWEPT_BODY",BODY,{"disambiguationData":[OSD([sQuery(id+"F0.wireOp",EDGE,"E1")])]}),"instanceName":"1"}),"instanceName":"1"}),"instanceName":"1"}),"instanceName":"1"});
            var Q1848;
            Q1848=makeQuery(id+"F13.opPattern","COPY",BODY,{"derivedFrom":makeQuery(id+"F10.opPattern","COPY",BODY,{"derivedFrom":makeQuery(id+"F9.opPattern","COPY",BODY,{"derivedFrom":makeQuery(id+"F7.opPattern","COPY",BODY,{"derivedFrom":makeQuery(id+"F2.opPattern","COPY",BODY,{"derivedFrom":makeQuery(id+"F1.opRevolve","SWEPT_BODY",BODY,{"disambiguationData":[OSD([sQuery(id+"F0.wireOp",EDGE,"E1")])]}),"instanceName":"1"}),"instanceName":"1"}),"instanceName":"1"}),"instanceName":"1"}),"instanceName":"1"});
            var Q1849;
            Q1849=makeQuery(id+"F13.opPattern","COPY",BODY,{"derivedFrom":makeQuery(id+"F10.opPattern","COPY",BODY,{"derivedFrom":makeQuery(id+"F9.opPattern","COPY",BODY,{"derivedFrom":makeQuery(id+"F7.opPattern","COPY",BODY,{"derivedFrom":makeQuery(id+"F3.opPattern","COPY",BODY,{"derivedFrom":makeQuery(id+"F2.opPattern","COPY",BODY,{"derivedFrom":makeQuery(id+"F1.opRevolve","SWEPT_BODY",BODY,{"disambiguationData":[OSD([sQuery(id+"F0.wireOp",EDGE,"E1")])]}),"instanceName":"1"}),"instanceName":"1"}),"instanceName":"1"}),"instanceName":"1"}),"instanceName":"1"}),"instanceName":"1"});
            var Q1850;
            Q1850=makeQuery(id+"F13.opPattern","COPY",BODY,{"derivedFrom":makeQuery(id+"F10.opPattern","COPY",BODY,{"derivedFrom":makeQuery(id+"F9.opPattern","COPY",BODY,{"derivedFrom":makeQuery(id+"F7.opPattern","COPY",BODY,{"derivedFrom":makeQuery(id+"F4.opPattern","COPY",BODY,{"derivedFrom":makeQuery(id+"F1.opRevolve","SWEPT_BODY",BODY,{"disambiguationData":[OSD([sQuery(id+"F0.wireOp",EDGE,"E1")])]}),"instanceName":"1"}),"instanceName":"1"}),"instanceName":"1"}),"instanceName":"1"}),"instanceName":"1"});
            var Q1851;
            Q1851=makeQuery(id+"F13.opPattern","COPY",BODY,{"derivedFrom":makeQuery(id+"F10.opPattern","COPY",BODY,{"derivedFrom":makeQuery(id+"F9.opPattern","COPY",BODY,{"derivedFrom":makeQuery(id+"F7.opPattern","COPY",BODY,{"derivedFrom":makeQuery(id+"F4.opPattern","COPY",BODY,{"derivedFrom":makeQuery(id+"F2.opPattern","COPY",BODY,{"derivedFrom":makeQuery(id+"F1.opRevolve","SWEPT_BODY",BODY,{"disambiguationData":[OSD([sQuery(id+"F0.wireOp",EDGE,"E1")])]}),"instanceName":"1"}),"instanceName":"1"}),"instanceName":"1"}),"instanceName":"1"}),"instanceName":"1"}),"instanceName":"1"});
            var Q1852;
            Q1852=makeQuery(id+"F13.opPattern","COPY",BODY,{"derivedFrom":makeQuery(id+"F10.opPattern","COPY",BODY,{"derivedFrom":makeQuery(id+"F9.opPattern","COPY",BODY,{"derivedFrom":makeQuery(id+"F7.opPattern","COPY",BODY,{"derivedFrom":makeQuery(id+"F4.opPattern","COPY",BODY,{"derivedFrom":makeQuery(id+"F3.opPattern","COPY",BODY,{"derivedFrom":makeQuery(id+"F2.opPattern","COPY",BODY,{"derivedFrom":makeQuery(id+"F1.opRevolve","SWEPT_BODY",BODY,{"disambiguationData":[OSD([sQuery(id+"F0.wireOp",EDGE,"E1")])]}),"instanceName":"1"}),"instanceName":"1"}),"instanceName":"1"}),"instanceName":"1"}),"instanceName":"1"}),"instanceName":"1"}),"instanceName":"1"});
            var Q1853;
            Q1853=makeQuery(id+"F13.opPattern","COPY",BODY,{"derivedFrom":makeQuery(id+"F10.opPattern","COPY",BODY,{"derivedFrom":makeQuery(id+"F9.opPattern","COPY",BODY,{"derivedFrom":makeQuery(id+"F7.opPattern","COPY",BODY,{"derivedFrom":makeQuery(id+"F5.opPattern","COPY",BODY,{"derivedFrom":makeQuery(id+"F1.opRevolve","SWEPT_BODY",BODY,{"disambiguationData":[OSD([sQuery(id+"F0.wireOp",EDGE,"E1")])]}),"instanceName":"1"}),"instanceName":"1"}),"instanceName":"1"}),"instanceName":"1"}),"instanceName":"1"});
            var Q1854;
            Q1854=makeQuery(id+"F13.opPattern","COPY",BODY,{"derivedFrom":makeQuery(id+"F10.opPattern","COPY",BODY,{"derivedFrom":makeQuery(id+"F9.opPattern","COPY",BODY,{"derivedFrom":makeQuery(id+"F7.opPattern","COPY",BODY,{"derivedFrom":makeQuery(id+"F5.opPattern","COPY",BODY,{"derivedFrom":makeQuery(id+"F2.opPattern","COPY",BODY,{"derivedFrom":makeQuery(id+"F1.opRevolve","SWEPT_BODY",BODY,{"disambiguationData":[OSD([sQuery(id+"F0.wireOp",EDGE,"E1")])]}),"instanceName":"1"}),"instanceName":"1"}),"instanceName":"1"}),"instanceName":"1"}),"instanceName":"1"}),"instanceName":"1"});
            var Q1855;
            Q1855=makeQuery(id+"F13.opPattern","COPY",BODY,{"derivedFrom":makeQuery(id+"F10.opPattern","COPY",BODY,{"derivedFrom":makeQuery(id+"F9.opPattern","COPY",BODY,{"derivedFrom":makeQuery(id+"F7.opPattern","COPY",BODY,{"derivedFrom":makeQuery(id+"F5.opPattern","COPY",BODY,{"derivedFrom":makeQuery(id+"F3.opPattern","COPY",BODY,{"derivedFrom":makeQuery(id+"F2.opPattern","COPY",BODY,{"derivedFrom":makeQuery(id+"F1.opRevolve","SWEPT_BODY",BODY,{"disambiguationData":[OSD([sQuery(id+"F0.wireOp",EDGE,"E1")])]}),"instanceName":"1"}),"instanceName":"1"}),"instanceName":"1"}),"instanceName":"1"}),"instanceName":"1"}),"instanceName":"1"}),"instanceName":"1"});
            var Q1856;
            Q1856=makeQuery(id+"F13.opPattern","COPY",BODY,{"derivedFrom":makeQuery(id+"F10.opPattern","COPY",BODY,{"derivedFrom":makeQuery(id+"F9.opPattern","COPY",BODY,{"derivedFrom":makeQuery(id+"F7.opPattern","COPY",BODY,{"derivedFrom":makeQuery(id+"F5.opPattern","COPY",BODY,{"derivedFrom":makeQuery(id+"F4.opPattern","COPY",BODY,{"derivedFrom":makeQuery(id+"F1.opRevolve","SWEPT_BODY",BODY,{"disambiguationData":[OSD([sQuery(id+"F0.wireOp",EDGE,"E1")])]}),"instanceName":"1"}),"instanceName":"1"}),"instanceName":"1"}),"instanceName":"1"}),"instanceName":"1"}),"instanceName":"1"});
            var Q1857;
            Q1857=makeQuery(id+"F13.opPattern","COPY",BODY,{"derivedFrom":makeQuery(id+"F10.opPattern","COPY",BODY,{"derivedFrom":makeQuery(id+"F9.opPattern","COPY",BODY,{"derivedFrom":makeQuery(id+"F7.opPattern","COPY",BODY,{"derivedFrom":makeQuery(id+"F5.opPattern","COPY",BODY,{"derivedFrom":makeQuery(id+"F4.opPattern","COPY",BODY,{"derivedFrom":makeQuery(id+"F2.opPattern","COPY",BODY,{"derivedFrom":makeQuery(id+"F1.opRevolve","SWEPT_BODY",BODY,{"disambiguationData":[OSD([sQuery(id+"F0.wireOp",EDGE,"E1")])]}),"instanceName":"1"}),"instanceName":"1"}),"instanceName":"1"}),"instanceName":"1"}),"instanceName":"1"}),"instanceName":"1"}),"instanceName":"1"});
            var Q1858;
            Q1858=makeQuery(id+"F13.opPattern","COPY",BODY,{"derivedFrom":makeQuery(id+"F10.opPattern","COPY",BODY,{"derivedFrom":makeQuery(id+"F9.opPattern","COPY",BODY,{"derivedFrom":makeQuery(id+"F7.opPattern","COPY",BODY,{"derivedFrom":makeQuery(id+"F5.opPattern","COPY",BODY,{"derivedFrom":makeQuery(id+"F4.opPattern","COPY",BODY,{"derivedFrom":makeQuery(id+"F3.opPattern","COPY",BODY,{"derivedFrom":makeQuery(id+"F2.opPattern","COPY",BODY,{"derivedFrom":makeQuery(id+"F1.opRevolve","SWEPT_BODY",BODY,{"disambiguationData":[OSD([sQuery(id+"F0.wireOp",EDGE,"E1")])]}),"instanceName":"1"}),"instanceName":"1"}),"instanceName":"1"}),"instanceName":"1"}),"instanceName":"1"}),"instanceName":"1"}),"instanceName":"1"}),"instanceName":"1"});
            var Q1859;
            Q1859=makeQuery(id+"F13.opPattern","COPY",BODY,{"derivedFrom":makeQuery(id+"F10.opPattern","COPY",BODY,{"derivedFrom":makeQuery(id+"F9.opPattern","COPY",BODY,{"derivedFrom":makeQuery(id+"F7.opPattern","COPY",BODY,{"derivedFrom":makeQuery(id+"F6.opPattern","COPY",BODY,{"derivedFrom":makeQuery(id+"F1.opRevolve","SWEPT_BODY",BODY,{"disambiguationData":[OSD([sQuery(id+"F0.wireOp",EDGE,"E1")])]}),"instanceName":"1"}),"instanceName":"1"}),"instanceName":"1"}),"instanceName":"1"}),"instanceName":"1"});
            var Q1860;
            Q1860=makeQuery(id+"F13.opPattern","COPY",BODY,{"derivedFrom":makeQuery(id+"F10.opPattern","COPY",BODY,{"derivedFrom":makeQuery(id+"F9.opPattern","COPY",BODY,{"derivedFrom":makeQuery(id+"F7.opPattern","COPY",BODY,{"derivedFrom":makeQuery(id+"F6.opPattern","COPY",BODY,{"derivedFrom":makeQuery(id+"F2.opPattern","COPY",BODY,{"derivedFrom":makeQuery(id+"F1.opRevolve","SWEPT_BODY",BODY,{"disambiguationData":[OSD([sQuery(id+"F0.wireOp",EDGE,"E1")])]}),"instanceName":"1"}),"instanceName":"1"}),"instanceName":"1"}),"instanceName":"1"}),"instanceName":"1"}),"instanceName":"1"});
            var Q1861;
            Q1861=makeQuery(id+"F13.opPattern","COPY",BODY,{"derivedFrom":makeQuery(id+"F10.opPattern","COPY",BODY,{"derivedFrom":makeQuery(id+"F9.opPattern","COPY",BODY,{"derivedFrom":makeQuery(id+"F7.opPattern","COPY",BODY,{"derivedFrom":makeQuery(id+"F6.opPattern","COPY",BODY,{"derivedFrom":makeQuery(id+"F3.opPattern","COPY",BODY,{"derivedFrom":makeQuery(id+"F2.opPattern","COPY",BODY,{"derivedFrom":makeQuery(id+"F1.opRevolve","SWEPT_BODY",BODY,{"disambiguationData":[OSD([sQuery(id+"F0.wireOp",EDGE,"E1")])]}),"instanceName":"1"}),"instanceName":"1"}),"instanceName":"1"}),"instanceName":"1"}),"instanceName":"1"}),"instanceName":"1"}),"instanceName":"1"});
            var Q1862;
            Q1862=makeQuery(id+"F13.opPattern","COPY",BODY,{"derivedFrom":makeQuery(id+"F10.opPattern","COPY",BODY,{"derivedFrom":makeQuery(id+"F9.opPattern","COPY",BODY,{"derivedFrom":makeQuery(id+"F7.opPattern","COPY",BODY,{"derivedFrom":makeQuery(id+"F6.opPattern","COPY",BODY,{"derivedFrom":makeQuery(id+"F4.opPattern","COPY",BODY,{"derivedFrom":makeQuery(id+"F1.opRevolve","SWEPT_BODY",BODY,{"disambiguationData":[OSD([sQuery(id+"F0.wireOp",EDGE,"E1")])]}),"instanceName":"1"}),"instanceName":"1"}),"instanceName":"1"}),"instanceName":"1"}),"instanceName":"1"}),"instanceName":"1"});
            var Q1863;
            Q1863=makeQuery(id+"F13.opPattern","COPY",BODY,{"derivedFrom":makeQuery(id+"F10.opPattern","COPY",BODY,{"derivedFrom":makeQuery(id+"F9.opPattern","COPY",BODY,{"derivedFrom":makeQuery(id+"F7.opPattern","COPY",BODY,{"derivedFrom":makeQuery(id+"F6.opPattern","COPY",BODY,{"derivedFrom":makeQuery(id+"F4.opPattern","COPY",BODY,{"derivedFrom":makeQuery(id+"F2.opPattern","COPY",BODY,{"derivedFrom":makeQuery(id+"F1.opRevolve","SWEPT_BODY",BODY,{"disambiguationData":[OSD([sQuery(id+"F0.wireOp",EDGE,"E1")])]}),"instanceName":"1"}),"instanceName":"1"}),"instanceName":"1"}),"instanceName":"1"}),"instanceName":"1"}),"instanceName":"1"}),"instanceName":"1"});
            var Q1864;
            Q1864=makeQuery(id+"F13.opPattern","COPY",BODY,{"derivedFrom":makeQuery(id+"F10.opPattern","COPY",BODY,{"derivedFrom":makeQuery(id+"F9.opPattern","COPY",BODY,{"derivedFrom":makeQuery(id+"F7.opPattern","COPY",BODY,{"derivedFrom":makeQuery(id+"F6.opPattern","COPY",BODY,{"derivedFrom":makeQuery(id+"F4.opPattern","COPY",BODY,{"derivedFrom":makeQuery(id+"F3.opPattern","COPY",BODY,{"derivedFrom":makeQuery(id+"F2.opPattern","COPY",BODY,{"derivedFrom":makeQuery(id+"F1.opRevolve","SWEPT_BODY",BODY,{"disambiguationData":[OSD([sQuery(id+"F0.wireOp",EDGE,"E1")])]}),"instanceName":"1"}),"instanceName":"1"}),"instanceName":"1"}),"instanceName":"1"}),"instanceName":"1"}),"instanceName":"1"}),"instanceName":"1"}),"instanceName":"1"});
            var Q1865;
            Q1865=makeQuery(id+"F13.opPattern","COPY",BODY,{"derivedFrom":makeQuery(id+"F10.opPattern","COPY",BODY,{"derivedFrom":makeQuery(id+"F9.opPattern","COPY",BODY,{"derivedFrom":makeQuery(id+"F7.opPattern","COPY",BODY,{"derivedFrom":makeQuery(id+"F6.opPattern","COPY",BODY,{"derivedFrom":makeQuery(id+"F5.opPattern","COPY",BODY,{"derivedFrom":makeQuery(id+"F1.opRevolve","SWEPT_BODY",BODY,{"disambiguationData":[OSD([sQuery(id+"F0.wireOp",EDGE,"E1")])]}),"instanceName":"1"}),"instanceName":"1"}),"instanceName":"1"}),"instanceName":"1"}),"instanceName":"1"}),"instanceName":"1"});
            var Q1866;
            Q1866=makeQuery(id+"F13.opPattern","COPY",BODY,{"derivedFrom":makeQuery(id+"F10.opPattern","COPY",BODY,{"derivedFrom":makeQuery(id+"F9.opPattern","COPY",BODY,{"derivedFrom":makeQuery(id+"F7.opPattern","COPY",BODY,{"derivedFrom":makeQuery(id+"F6.opPattern","COPY",BODY,{"derivedFrom":makeQuery(id+"F5.opPattern","COPY",BODY,{"derivedFrom":makeQuery(id+"F2.opPattern","COPY",BODY,{"derivedFrom":makeQuery(id+"F1.opRevolve","SWEPT_BODY",BODY,{"disambiguationData":[OSD([sQuery(id+"F0.wireOp",EDGE,"E1")])]}),"instanceName":"1"}),"instanceName":"1"}),"instanceName":"1"}),"instanceName":"1"}),"instanceName":"1"}),"instanceName":"1"}),"instanceName":"1"});
            var Q1867;
            Q1867=makeQuery(id+"F13.opPattern","COPY",BODY,{"derivedFrom":makeQuery(id+"F10.opPattern","COPY",BODY,{"derivedFrom":makeQuery(id+"F9.opPattern","COPY",BODY,{"derivedFrom":makeQuery(id+"F7.opPattern","COPY",BODY,{"derivedFrom":makeQuery(id+"F6.opPattern","COPY",BODY,{"derivedFrom":makeQuery(id+"F5.opPattern","COPY",BODY,{"derivedFrom":makeQuery(id+"F3.opPattern","COPY",BODY,{"derivedFrom":makeQuery(id+"F2.opPattern","COPY",BODY,{"derivedFrom":makeQuery(id+"F1.opRevolve","SWEPT_BODY",BODY,{"disambiguationData":[OSD([sQuery(id+"F0.wireOp",EDGE,"E1")])]}),"instanceName":"1"}),"instanceName":"1"}),"instanceName":"1"}),"instanceName":"1"}),"instanceName":"1"}),"instanceName":"1"}),"instanceName":"1"}),"instanceName":"1"});
            var Q1868;
            Q1868=makeQuery(id+"F13.opPattern","COPY",BODY,{"derivedFrom":makeQuery(id+"F10.opPattern","COPY",BODY,{"derivedFrom":makeQuery(id+"F9.opPattern","COPY",BODY,{"derivedFrom":makeQuery(id+"F7.opPattern","COPY",BODY,{"derivedFrom":makeQuery(id+"F6.opPattern","COPY",BODY,{"derivedFrom":makeQuery(id+"F5.opPattern","COPY",BODY,{"derivedFrom":makeQuery(id+"F4.opPattern","COPY",BODY,{"derivedFrom":makeQuery(id+"F1.opRevolve","SWEPT_BODY",BODY,{"disambiguationData":[OSD([sQuery(id+"F0.wireOp",EDGE,"E1")])]}),"instanceName":"1"}),"instanceName":"1"}),"instanceName":"1"}),"instanceName":"1"}),"instanceName":"1"}),"instanceName":"1"}),"instanceName":"1"});
            var Q1869;
            Q1869=makeQuery(id+"F13.opPattern","COPY",BODY,{"derivedFrom":makeQuery(id+"F10.opPattern","COPY",BODY,{"derivedFrom":makeQuery(id+"F9.opPattern","COPY",BODY,{"derivedFrom":makeQuery(id+"F7.opPattern","COPY",BODY,{"derivedFrom":makeQuery(id+"F6.opPattern","COPY",BODY,{"derivedFrom":makeQuery(id+"F5.opPattern","COPY",BODY,{"derivedFrom":makeQuery(id+"F4.opPattern","COPY",BODY,{"derivedFrom":makeQuery(id+"F2.opPattern","COPY",BODY,{"derivedFrom":makeQuery(id+"F1.opRevolve","SWEPT_BODY",BODY,{"disambiguationData":[OSD([sQuery(id+"F0.wireOp",EDGE,"E1")])]}),"instanceName":"1"}),"instanceName":"1"}),"instanceName":"1"}),"instanceName":"1"}),"instanceName":"1"}),"instanceName":"1"}),"instanceName":"1"}),"instanceName":"1"});
            var Q1870;
            Q1870=makeQuery(id+"F13.opPattern","COPY",BODY,{"derivedFrom":makeQuery(id+"F10.opPattern","COPY",BODY,{"derivedFrom":makeQuery(id+"F9.opPattern","COPY",BODY,{"derivedFrom":makeQuery(id+"F7.opPattern","COPY",BODY,{"derivedFrom":makeQuery(id+"F6.opPattern","COPY",BODY,{"derivedFrom":makeQuery(id+"F5.opPattern","COPY",BODY,{"derivedFrom":makeQuery(id+"F4.opPattern","COPY",BODY,{"derivedFrom":makeQuery(id+"F3.opPattern","COPY",BODY,{"derivedFrom":makeQuery(id+"F2.opPattern","COPY",BODY,{"derivedFrom":makeQuery(id+"F1.opRevolve","SWEPT_BODY",BODY,{"disambiguationData":[OSD([sQuery(id+"F0.wireOp",EDGE,"E1")])]}),"instanceName":"1"}),"instanceName":"1"}),"instanceName":"1"}),"instanceName":"1"}),"instanceName":"1"}),"instanceName":"1"}),"instanceName":"1"}),"instanceName":"1"}),"instanceName":"1"});
            var Q1871;
            Q1871=makeQuery(id+"F13.opPattern","COPY",BODY,{"derivedFrom":makeQuery(id+"F10.opPattern","COPY",BODY,{"derivedFrom":makeQuery(id+"F9.opPattern","COPY",BODY,{"derivedFrom":makeQuery(id+"F8.opPattern","COPY",BODY,{"derivedFrom":makeQuery(id+"F1.opRevolve","SWEPT_BODY",BODY,{"disambiguationData":[OSD([sQuery(id+"F0.wireOp",EDGE,"E1")])]}),"instanceName":"1"}),"instanceName":"1"}),"instanceName":"1"}),"instanceName":"1"});
            var Q1872;
            Q1872=makeQuery(id+"F13.opPattern","COPY",BODY,{"derivedFrom":makeQuery(id+"F10.opPattern","COPY",BODY,{"derivedFrom":makeQuery(id+"F9.opPattern","COPY",BODY,{"derivedFrom":makeQuery(id+"F8.opPattern","COPY",BODY,{"derivedFrom":makeQuery(id+"F2.opPattern","COPY",BODY,{"derivedFrom":makeQuery(id+"F1.opRevolve","SWEPT_BODY",BODY,{"disambiguationData":[OSD([sQuery(id+"F0.wireOp",EDGE,"E1")])]}),"instanceName":"1"}),"instanceName":"1"}),"instanceName":"1"}),"instanceName":"1"}),"instanceName":"1"});
            var Q1873;
            Q1873=makeQuery(id+"F13.opPattern","COPY",BODY,{"derivedFrom":makeQuery(id+"F10.opPattern","COPY",BODY,{"derivedFrom":makeQuery(id+"F9.opPattern","COPY",BODY,{"derivedFrom":makeQuery(id+"F8.opPattern","COPY",BODY,{"derivedFrom":makeQuery(id+"F3.opPattern","COPY",BODY,{"derivedFrom":makeQuery(id+"F2.opPattern","COPY",BODY,{"derivedFrom":makeQuery(id+"F1.opRevolve","SWEPT_BODY",BODY,{"disambiguationData":[OSD([sQuery(id+"F0.wireOp",EDGE,"E1")])]}),"instanceName":"1"}),"instanceName":"1"}),"instanceName":"1"}),"instanceName":"1"}),"instanceName":"1"}),"instanceName":"1"});
            var Q1874;
            Q1874=makeQuery(id+"F13.opPattern","COPY",BODY,{"derivedFrom":makeQuery(id+"F10.opPattern","COPY",BODY,{"derivedFrom":makeQuery(id+"F9.opPattern","COPY",BODY,{"derivedFrom":makeQuery(id+"F8.opPattern","COPY",BODY,{"derivedFrom":makeQuery(id+"F4.opPattern","COPY",BODY,{"derivedFrom":makeQuery(id+"F1.opRevolve","SWEPT_BODY",BODY,{"disambiguationData":[OSD([sQuery(id+"F0.wireOp",EDGE,"E1")])]}),"instanceName":"1"}),"instanceName":"1"}),"instanceName":"1"}),"instanceName":"1"}),"instanceName":"1"});
            var Q1875;
            Q1875=makeQuery(id+"F13.opPattern","COPY",BODY,{"derivedFrom":makeQuery(id+"F10.opPattern","COPY",BODY,{"derivedFrom":makeQuery(id+"F9.opPattern","COPY",BODY,{"derivedFrom":makeQuery(id+"F8.opPattern","COPY",BODY,{"derivedFrom":makeQuery(id+"F4.opPattern","COPY",BODY,{"derivedFrom":makeQuery(id+"F2.opPattern","COPY",BODY,{"derivedFrom":makeQuery(id+"F1.opRevolve","SWEPT_BODY",BODY,{"disambiguationData":[OSD([sQuery(id+"F0.wireOp",EDGE,"E1")])]}),"instanceName":"1"}),"instanceName":"1"}),"instanceName":"1"}),"instanceName":"1"}),"instanceName":"1"}),"instanceName":"1"});
            var Q1876;
            Q1876=makeQuery(id+"F13.opPattern","COPY",BODY,{"derivedFrom":makeQuery(id+"F10.opPattern","COPY",BODY,{"derivedFrom":makeQuery(id+"F9.opPattern","COPY",BODY,{"derivedFrom":makeQuery(id+"F8.opPattern","COPY",BODY,{"derivedFrom":makeQuery(id+"F4.opPattern","COPY",BODY,{"derivedFrom":makeQuery(id+"F3.opPattern","COPY",BODY,{"derivedFrom":makeQuery(id+"F2.opPattern","COPY",BODY,{"derivedFrom":makeQuery(id+"F1.opRevolve","SWEPT_BODY",BODY,{"disambiguationData":[OSD([sQuery(id+"F0.wireOp",EDGE,"E1")])]}),"instanceName":"1"}),"instanceName":"1"}),"instanceName":"1"}),"instanceName":"1"}),"instanceName":"1"}),"instanceName":"1"}),"instanceName":"1"});
            var Q1877;
            Q1877=makeQuery(id+"F13.opPattern","COPY",BODY,{"derivedFrom":makeQuery(id+"F10.opPattern","COPY",BODY,{"derivedFrom":makeQuery(id+"F9.opPattern","COPY",BODY,{"derivedFrom":makeQuery(id+"F8.opPattern","COPY",BODY,{"derivedFrom":makeQuery(id+"F5.opPattern","COPY",BODY,{"derivedFrom":makeQuery(id+"F1.opRevolve","SWEPT_BODY",BODY,{"disambiguationData":[OSD([sQuery(id+"F0.wireOp",EDGE,"E1")])]}),"instanceName":"1"}),"instanceName":"1"}),"instanceName":"1"}),"instanceName":"1"}),"instanceName":"1"});
            var Q1878;
            Q1878=makeQuery(id+"F13.opPattern","COPY",BODY,{"derivedFrom":makeQuery(id+"F10.opPattern","COPY",BODY,{"derivedFrom":makeQuery(id+"F9.opPattern","COPY",BODY,{"derivedFrom":makeQuery(id+"F8.opPattern","COPY",BODY,{"derivedFrom":makeQuery(id+"F5.opPattern","COPY",BODY,{"derivedFrom":makeQuery(id+"F2.opPattern","COPY",BODY,{"derivedFrom":makeQuery(id+"F1.opRevolve","SWEPT_BODY",BODY,{"disambiguationData":[OSD([sQuery(id+"F0.wireOp",EDGE,"E1")])]}),"instanceName":"1"}),"instanceName":"1"}),"instanceName":"1"}),"instanceName":"1"}),"instanceName":"1"}),"instanceName":"1"});
            var Q1879;
            Q1879=makeQuery(id+"F13.opPattern","COPY",BODY,{"derivedFrom":makeQuery(id+"F10.opPattern","COPY",BODY,{"derivedFrom":makeQuery(id+"F9.opPattern","COPY",BODY,{"derivedFrom":makeQuery(id+"F8.opPattern","COPY",BODY,{"derivedFrom":makeQuery(id+"F5.opPattern","COPY",BODY,{"derivedFrom":makeQuery(id+"F3.opPattern","COPY",BODY,{"derivedFrom":makeQuery(id+"F2.opPattern","COPY",BODY,{"derivedFrom":makeQuery(id+"F1.opRevolve","SWEPT_BODY",BODY,{"disambiguationData":[OSD([sQuery(id+"F0.wireOp",EDGE,"E1")])]}),"instanceName":"1"}),"instanceName":"1"}),"instanceName":"1"}),"instanceName":"1"}),"instanceName":"1"}),"instanceName":"1"}),"instanceName":"1"});
            var Q1880;
            Q1880=makeQuery(id+"F13.opPattern","COPY",BODY,{"derivedFrom":makeQuery(id+"F10.opPattern","COPY",BODY,{"derivedFrom":makeQuery(id+"F9.opPattern","COPY",BODY,{"derivedFrom":makeQuery(id+"F8.opPattern","COPY",BODY,{"derivedFrom":makeQuery(id+"F5.opPattern","COPY",BODY,{"derivedFrom":makeQuery(id+"F4.opPattern","COPY",BODY,{"derivedFrom":makeQuery(id+"F1.opRevolve","SWEPT_BODY",BODY,{"disambiguationData":[OSD([sQuery(id+"F0.wireOp",EDGE,"E1")])]}),"instanceName":"1"}),"instanceName":"1"}),"instanceName":"1"}),"instanceName":"1"}),"instanceName":"1"}),"instanceName":"1"});
            var Q1881;
            Q1881=makeQuery(id+"F13.opPattern","COPY",BODY,{"derivedFrom":makeQuery(id+"F10.opPattern","COPY",BODY,{"derivedFrom":makeQuery(id+"F9.opPattern","COPY",BODY,{"derivedFrom":makeQuery(id+"F8.opPattern","COPY",BODY,{"derivedFrom":makeQuery(id+"F5.opPattern","COPY",BODY,{"derivedFrom":makeQuery(id+"F4.opPattern","COPY",BODY,{"derivedFrom":makeQuery(id+"F2.opPattern","COPY",BODY,{"derivedFrom":makeQuery(id+"F1.opRevolve","SWEPT_BODY",BODY,{"disambiguationData":[OSD([sQuery(id+"F0.wireOp",EDGE,"E1")])]}),"instanceName":"1"}),"instanceName":"1"}),"instanceName":"1"}),"instanceName":"1"}),"instanceName":"1"}),"instanceName":"1"}),"instanceName":"1"});
            var Q1882;
            Q1882=makeQuery(id+"F13.opPattern","COPY",BODY,{"derivedFrom":makeQuery(id+"F10.opPattern","COPY",BODY,{"derivedFrom":makeQuery(id+"F9.opPattern","COPY",BODY,{"derivedFrom":makeQuery(id+"F8.opPattern","COPY",BODY,{"derivedFrom":makeQuery(id+"F5.opPattern","COPY",BODY,{"derivedFrom":makeQuery(id+"F4.opPattern","COPY",BODY,{"derivedFrom":makeQuery(id+"F3.opPattern","COPY",BODY,{"derivedFrom":makeQuery(id+"F2.opPattern","COPY",BODY,{"derivedFrom":makeQuery(id+"F1.opRevolve","SWEPT_BODY",BODY,{"disambiguationData":[OSD([sQuery(id+"F0.wireOp",EDGE,"E1")])]}),"instanceName":"1"}),"instanceName":"1"}),"instanceName":"1"}),"instanceName":"1"}),"instanceName":"1"}),"instanceName":"1"}),"instanceName":"1"}),"instanceName":"1"});
            var Q1883;
            Q1883=makeQuery(id+"F13.opPattern","COPY",BODY,{"derivedFrom":makeQuery(id+"F10.opPattern","COPY",BODY,{"derivedFrom":makeQuery(id+"F9.opPattern","COPY",BODY,{"derivedFrom":makeQuery(id+"F8.opPattern","COPY",BODY,{"derivedFrom":makeQuery(id+"F6.opPattern","COPY",BODY,{"derivedFrom":makeQuery(id+"F1.opRevolve","SWEPT_BODY",BODY,{"disambiguationData":[OSD([sQuery(id+"F0.wireOp",EDGE,"E1")])]}),"instanceName":"1"}),"instanceName":"1"}),"instanceName":"1"}),"instanceName":"1"}),"instanceName":"1"});
            var Q1884;
            Q1884=makeQuery(id+"F13.opPattern","COPY",BODY,{"derivedFrom":makeQuery(id+"F10.opPattern","COPY",BODY,{"derivedFrom":makeQuery(id+"F9.opPattern","COPY",BODY,{"derivedFrom":makeQuery(id+"F8.opPattern","COPY",BODY,{"derivedFrom":makeQuery(id+"F6.opPattern","COPY",BODY,{"derivedFrom":makeQuery(id+"F2.opPattern","COPY",BODY,{"derivedFrom":makeQuery(id+"F1.opRevolve","SWEPT_BODY",BODY,{"disambiguationData":[OSD([sQuery(id+"F0.wireOp",EDGE,"E1")])]}),"instanceName":"1"}),"instanceName":"1"}),"instanceName":"1"}),"instanceName":"1"}),"instanceName":"1"}),"instanceName":"1"});
            var Q1885;
            Q1885=makeQuery(id+"F13.opPattern","COPY",BODY,{"derivedFrom":makeQuery(id+"F10.opPattern","COPY",BODY,{"derivedFrom":makeQuery(id+"F9.opPattern","COPY",BODY,{"derivedFrom":makeQuery(id+"F8.opPattern","COPY",BODY,{"derivedFrom":makeQuery(id+"F6.opPattern","COPY",BODY,{"derivedFrom":makeQuery(id+"F3.opPattern","COPY",BODY,{"derivedFrom":makeQuery(id+"F2.opPattern","COPY",BODY,{"derivedFrom":makeQuery(id+"F1.opRevolve","SWEPT_BODY",BODY,{"disambiguationData":[OSD([sQuery(id+"F0.wireOp",EDGE,"E1")])]}),"instanceName":"1"}),"instanceName":"1"}),"instanceName":"1"}),"instanceName":"1"}),"instanceName":"1"}),"instanceName":"1"}),"instanceName":"1"});
            var Q1886;
            Q1886=makeQuery(id+"F13.opPattern","COPY",BODY,{"derivedFrom":makeQuery(id+"F10.opPattern","COPY",BODY,{"derivedFrom":makeQuery(id+"F9.opPattern","COPY",BODY,{"derivedFrom":makeQuery(id+"F8.opPattern","COPY",BODY,{"derivedFrom":makeQuery(id+"F6.opPattern","COPY",BODY,{"derivedFrom":makeQuery(id+"F4.opPattern","COPY",BODY,{"derivedFrom":makeQuery(id+"F1.opRevolve","SWEPT_BODY",BODY,{"disambiguationData":[OSD([sQuery(id+"F0.wireOp",EDGE,"E1")])]}),"instanceName":"1"}),"instanceName":"1"}),"instanceName":"1"}),"instanceName":"1"}),"instanceName":"1"}),"instanceName":"1"});
            var Q1887;
            Q1887=makeQuery(id+"F13.opPattern","COPY",BODY,{"derivedFrom":makeQuery(id+"F10.opPattern","COPY",BODY,{"derivedFrom":makeQuery(id+"F9.opPattern","COPY",BODY,{"derivedFrom":makeQuery(id+"F8.opPattern","COPY",BODY,{"derivedFrom":makeQuery(id+"F6.opPattern","COPY",BODY,{"derivedFrom":makeQuery(id+"F4.opPattern","COPY",BODY,{"derivedFrom":makeQuery(id+"F2.opPattern","COPY",BODY,{"derivedFrom":makeQuery(id+"F1.opRevolve","SWEPT_BODY",BODY,{"disambiguationData":[OSD([sQuery(id+"F0.wireOp",EDGE,"E1")])]}),"instanceName":"1"}),"instanceName":"1"}),"instanceName":"1"}),"instanceName":"1"}),"instanceName":"1"}),"instanceName":"1"}),"instanceName":"1"});
            var Q1888;
            Q1888=makeQuery(id+"F13.opPattern","COPY",BODY,{"derivedFrom":makeQuery(id+"F10.opPattern","COPY",BODY,{"derivedFrom":makeQuery(id+"F9.opPattern","COPY",BODY,{"derivedFrom":makeQuery(id+"F8.opPattern","COPY",BODY,{"derivedFrom":makeQuery(id+"F6.opPattern","COPY",BODY,{"derivedFrom":makeQuery(id+"F4.opPattern","COPY",BODY,{"derivedFrom":makeQuery(id+"F3.opPattern","COPY",BODY,{"derivedFrom":makeQuery(id+"F2.opPattern","COPY",BODY,{"derivedFrom":makeQuery(id+"F1.opRevolve","SWEPT_BODY",BODY,{"disambiguationData":[OSD([sQuery(id+"F0.wireOp",EDGE,"E1")])]}),"instanceName":"1"}),"instanceName":"1"}),"instanceName":"1"}),"instanceName":"1"}),"instanceName":"1"}),"instanceName":"1"}),"instanceName":"1"}),"instanceName":"1"});
            var Q1889;
            Q1889=makeQuery(id+"F13.opPattern","COPY",BODY,{"derivedFrom":makeQuery(id+"F10.opPattern","COPY",BODY,{"derivedFrom":makeQuery(id+"F9.opPattern","COPY",BODY,{"derivedFrom":makeQuery(id+"F8.opPattern","COPY",BODY,{"derivedFrom":makeQuery(id+"F6.opPattern","COPY",BODY,{"derivedFrom":makeQuery(id+"F5.opPattern","COPY",BODY,{"derivedFrom":makeQuery(id+"F1.opRevolve","SWEPT_BODY",BODY,{"disambiguationData":[OSD([sQuery(id+"F0.wireOp",EDGE,"E1")])]}),"instanceName":"1"}),"instanceName":"1"}),"instanceName":"1"}),"instanceName":"1"}),"instanceName":"1"}),"instanceName":"1"});
            var Q1890;
            Q1890=makeQuery(id+"F13.opPattern","COPY",BODY,{"derivedFrom":makeQuery(id+"F10.opPattern","COPY",BODY,{"derivedFrom":makeQuery(id+"F9.opPattern","COPY",BODY,{"derivedFrom":makeQuery(id+"F8.opPattern","COPY",BODY,{"derivedFrom":makeQuery(id+"F6.opPattern","COPY",BODY,{"derivedFrom":makeQuery(id+"F5.opPattern","COPY",BODY,{"derivedFrom":makeQuery(id+"F2.opPattern","COPY",BODY,{"derivedFrom":makeQuery(id+"F1.opRevolve","SWEPT_BODY",BODY,{"disambiguationData":[OSD([sQuery(id+"F0.wireOp",EDGE,"E1")])]}),"instanceName":"1"}),"instanceName":"1"}),"instanceName":"1"}),"instanceName":"1"}),"instanceName":"1"}),"instanceName":"1"}),"instanceName":"1"});
            var Q1891;
            Q1891=makeQuery(id+"F13.opPattern","COPY",BODY,{"derivedFrom":makeQuery(id+"F10.opPattern","COPY",BODY,{"derivedFrom":makeQuery(id+"F9.opPattern","COPY",BODY,{"derivedFrom":makeQuery(id+"F8.opPattern","COPY",BODY,{"derivedFrom":makeQuery(id+"F6.opPattern","COPY",BODY,{"derivedFrom":makeQuery(id+"F5.opPattern","COPY",BODY,{"derivedFrom":makeQuery(id+"F3.opPattern","COPY",BODY,{"derivedFrom":makeQuery(id+"F2.opPattern","COPY",BODY,{"derivedFrom":makeQuery(id+"F1.opRevolve","SWEPT_BODY",BODY,{"disambiguationData":[OSD([sQuery(id+"F0.wireOp",EDGE,"E1")])]}),"instanceName":"1"}),"instanceName":"1"}),"instanceName":"1"}),"instanceName":"1"}),"instanceName":"1"}),"instanceName":"1"}),"instanceName":"1"}),"instanceName":"1"});
            var Q1892;
            Q1892=makeQuery(id+"F13.opPattern","COPY",BODY,{"derivedFrom":makeQuery(id+"F10.opPattern","COPY",BODY,{"derivedFrom":makeQuery(id+"F9.opPattern","COPY",BODY,{"derivedFrom":makeQuery(id+"F8.opPattern","COPY",BODY,{"derivedFrom":makeQuery(id+"F6.opPattern","COPY",BODY,{"derivedFrom":makeQuery(id+"F5.opPattern","COPY",BODY,{"derivedFrom":makeQuery(id+"F4.opPattern","COPY",BODY,{"derivedFrom":makeQuery(id+"F1.opRevolve","SWEPT_BODY",BODY,{"disambiguationData":[OSD([sQuery(id+"F0.wireOp",EDGE,"E1")])]}),"instanceName":"1"}),"instanceName":"1"}),"instanceName":"1"}),"instanceName":"1"}),"instanceName":"1"}),"instanceName":"1"}),"instanceName":"1"});
            var Q1893;
            Q1893=makeQuery(id+"F13.opPattern","COPY",BODY,{"derivedFrom":makeQuery(id+"F10.opPattern","COPY",BODY,{"derivedFrom":makeQuery(id+"F9.opPattern","COPY",BODY,{"derivedFrom":makeQuery(id+"F8.opPattern","COPY",BODY,{"derivedFrom":makeQuery(id+"F6.opPattern","COPY",BODY,{"derivedFrom":makeQuery(id+"F5.opPattern","COPY",BODY,{"derivedFrom":makeQuery(id+"F4.opPattern","COPY",BODY,{"derivedFrom":makeQuery(id+"F2.opPattern","COPY",BODY,{"derivedFrom":makeQuery(id+"F1.opRevolve","SWEPT_BODY",BODY,{"disambiguationData":[OSD([sQuery(id+"F0.wireOp",EDGE,"E1")])]}),"instanceName":"1"}),"instanceName":"1"}),"instanceName":"1"}),"instanceName":"1"}),"instanceName":"1"}),"instanceName":"1"}),"instanceName":"1"}),"instanceName":"1"});
            var Q1894;
            Q1894=makeQuery(id+"F13.opPattern","COPY",BODY,{"derivedFrom":makeQuery(id+"F10.opPattern","COPY",BODY,{"derivedFrom":makeQuery(id+"F9.opPattern","COPY",BODY,{"derivedFrom":makeQuery(id+"F8.opPattern","COPY",BODY,{"derivedFrom":makeQuery(id+"F6.opPattern","COPY",BODY,{"derivedFrom":makeQuery(id+"F5.opPattern","COPY",BODY,{"derivedFrom":makeQuery(id+"F4.opPattern","COPY",BODY,{"derivedFrom":makeQuery(id+"F3.opPattern","COPY",BODY,{"derivedFrom":makeQuery(id+"F2.opPattern","COPY",BODY,{"derivedFrom":makeQuery(id+"F1.opRevolve","SWEPT_BODY",BODY,{"disambiguationData":[OSD([sQuery(id+"F0.wireOp",EDGE,"E1")])]}),"instanceName":"1"}),"instanceName":"1"}),"instanceName":"1"}),"instanceName":"1"}),"instanceName":"1"}),"instanceName":"1"}),"instanceName":"1"}),"instanceName":"1"}),"instanceName":"1"});
            var Q1895;
            Q1895=makeQuery(id+"F13.opPattern","COPY",BODY,{"derivedFrom":makeQuery(id+"F10.opPattern","COPY",BODY,{"derivedFrom":makeQuery(id+"F9.opPattern","COPY",BODY,{"derivedFrom":makeQuery(id+"F8.opPattern","COPY",BODY,{"derivedFrom":makeQuery(id+"F7.opPattern","COPY",BODY,{"derivedFrom":makeQuery(id+"F1.opRevolve","SWEPT_BODY",BODY,{"disambiguationData":[OSD([sQuery(id+"F0.wireOp",EDGE,"E1")])]}),"instanceName":"1"}),"instanceName":"1"}),"instanceName":"1"}),"instanceName":"1"}),"instanceName":"1"});
            var Q1896;
            Q1896=makeQuery(id+"F13.opPattern","COPY",BODY,{"derivedFrom":makeQuery(id+"F10.opPattern","COPY",BODY,{"derivedFrom":makeQuery(id+"F9.opPattern","COPY",BODY,{"derivedFrom":makeQuery(id+"F8.opPattern","COPY",BODY,{"derivedFrom":makeQuery(id+"F7.opPattern","COPY",BODY,{"derivedFrom":makeQuery(id+"F2.opPattern","COPY",BODY,{"derivedFrom":makeQuery(id+"F1.opRevolve","SWEPT_BODY",BODY,{"disambiguationData":[OSD([sQuery(id+"F0.wireOp",EDGE,"E1")])]}),"instanceName":"1"}),"instanceName":"1"}),"instanceName":"1"}),"instanceName":"1"}),"instanceName":"1"}),"instanceName":"1"});
            var Q1897;
            Q1897=makeQuery(id+"F13.opPattern","COPY",BODY,{"derivedFrom":makeQuery(id+"F10.opPattern","COPY",BODY,{"derivedFrom":makeQuery(id+"F9.opPattern","COPY",BODY,{"derivedFrom":makeQuery(id+"F8.opPattern","COPY",BODY,{"derivedFrom":makeQuery(id+"F7.opPattern","COPY",BODY,{"derivedFrom":makeQuery(id+"F3.opPattern","COPY",BODY,{"derivedFrom":makeQuery(id+"F2.opPattern","COPY",BODY,{"derivedFrom":makeQuery(id+"F1.opRevolve","SWEPT_BODY",BODY,{"disambiguationData":[OSD([sQuery(id+"F0.wireOp",EDGE,"E1")])]}),"instanceName":"1"}),"instanceName":"1"}),"instanceName":"1"}),"instanceName":"1"}),"instanceName":"1"}),"instanceName":"1"}),"instanceName":"1"});
            var Q1898;
            Q1898=makeQuery(id+"F13.opPattern","COPY",BODY,{"derivedFrom":makeQuery(id+"F10.opPattern","COPY",BODY,{"derivedFrom":makeQuery(id+"F9.opPattern","COPY",BODY,{"derivedFrom":makeQuery(id+"F8.opPattern","COPY",BODY,{"derivedFrom":makeQuery(id+"F7.opPattern","COPY",BODY,{"derivedFrom":makeQuery(id+"F4.opPattern","COPY",BODY,{"derivedFrom":makeQuery(id+"F1.opRevolve","SWEPT_BODY",BODY,{"disambiguationData":[OSD([sQuery(id+"F0.wireOp",EDGE,"E1")])]}),"instanceName":"1"}),"instanceName":"1"}),"instanceName":"1"}),"instanceName":"1"}),"instanceName":"1"}),"instanceName":"1"});
            var Q1899;
            Q1899=makeQuery(id+"F13.opPattern","COPY",BODY,{"derivedFrom":makeQuery(id+"F10.opPattern","COPY",BODY,{"derivedFrom":makeQuery(id+"F9.opPattern","COPY",BODY,{"derivedFrom":makeQuery(id+"F8.opPattern","COPY",BODY,{"derivedFrom":makeQuery(id+"F7.opPattern","COPY",BODY,{"derivedFrom":makeQuery(id+"F4.opPattern","COPY",BODY,{"derivedFrom":makeQuery(id+"F2.opPattern","COPY",BODY,{"derivedFrom":makeQuery(id+"F1.opRevolve","SWEPT_BODY",BODY,{"disambiguationData":[OSD([sQuery(id+"F0.wireOp",EDGE,"E1")])]}),"instanceName":"1"}),"instanceName":"1"}),"instanceName":"1"}),"instanceName":"1"}),"instanceName":"1"}),"instanceName":"1"}),"instanceName":"1"});
            var Q1900;
            Q1900=makeQuery(id+"F13.opPattern","COPY",BODY,{"derivedFrom":makeQuery(id+"F10.opPattern","COPY",BODY,{"derivedFrom":makeQuery(id+"F9.opPattern","COPY",BODY,{"derivedFrom":makeQuery(id+"F8.opPattern","COPY",BODY,{"derivedFrom":makeQuery(id+"F7.opPattern","COPY",BODY,{"derivedFrom":makeQuery(id+"F4.opPattern","COPY",BODY,{"derivedFrom":makeQuery(id+"F3.opPattern","COPY",BODY,{"derivedFrom":makeQuery(id+"F2.opPattern","COPY",BODY,{"derivedFrom":makeQuery(id+"F1.opRevolve","SWEPT_BODY",BODY,{"disambiguationData":[OSD([sQuery(id+"F0.wireOp",EDGE,"E1")])]}),"instanceName":"1"}),"instanceName":"1"}),"instanceName":"1"}),"instanceName":"1"}),"instanceName":"1"}),"instanceName":"1"}),"instanceName":"1"}),"instanceName":"1"});
            var Q1901;
            Q1901=makeQuery(id+"F13.opPattern","COPY",BODY,{"derivedFrom":makeQuery(id+"F10.opPattern","COPY",BODY,{"derivedFrom":makeQuery(id+"F9.opPattern","COPY",BODY,{"derivedFrom":makeQuery(id+"F8.opPattern","COPY",BODY,{"derivedFrom":makeQuery(id+"F7.opPattern","COPY",BODY,{"derivedFrom":makeQuery(id+"F5.opPattern","COPY",BODY,{"derivedFrom":makeQuery(id+"F1.opRevolve","SWEPT_BODY",BODY,{"disambiguationData":[OSD([sQuery(id+"F0.wireOp",EDGE,"E1")])]}),"instanceName":"1"}),"instanceName":"1"}),"instanceName":"1"}),"instanceName":"1"}),"instanceName":"1"}),"instanceName":"1"});
            var Q1902;
            Q1902=makeQuery(id+"F13.opPattern","COPY",BODY,{"derivedFrom":makeQuery(id+"F10.opPattern","COPY",BODY,{"derivedFrom":makeQuery(id+"F9.opPattern","COPY",BODY,{"derivedFrom":makeQuery(id+"F8.opPattern","COPY",BODY,{"derivedFrom":makeQuery(id+"F7.opPattern","COPY",BODY,{"derivedFrom":makeQuery(id+"F5.opPattern","COPY",BODY,{"derivedFrom":makeQuery(id+"F2.opPattern","COPY",BODY,{"derivedFrom":makeQuery(id+"F1.opRevolve","SWEPT_BODY",BODY,{"disambiguationData":[OSD([sQuery(id+"F0.wireOp",EDGE,"E1")])]}),"instanceName":"1"}),"instanceName":"1"}),"instanceName":"1"}),"instanceName":"1"}),"instanceName":"1"}),"instanceName":"1"}),"instanceName":"1"});
            var Q1903;
            Q1903=makeQuery(id+"F13.opPattern","COPY",BODY,{"derivedFrom":makeQuery(id+"F10.opPattern","COPY",BODY,{"derivedFrom":makeQuery(id+"F9.opPattern","COPY",BODY,{"derivedFrom":makeQuery(id+"F8.opPattern","COPY",BODY,{"derivedFrom":makeQuery(id+"F7.opPattern","COPY",BODY,{"derivedFrom":makeQuery(id+"F5.opPattern","COPY",BODY,{"derivedFrom":makeQuery(id+"F3.opPattern","COPY",BODY,{"derivedFrom":makeQuery(id+"F2.opPattern","COPY",BODY,{"derivedFrom":makeQuery(id+"F1.opRevolve","SWEPT_BODY",BODY,{"disambiguationData":[OSD([sQuery(id+"F0.wireOp",EDGE,"E1")])]}),"instanceName":"1"}),"instanceName":"1"}),"instanceName":"1"}),"instanceName":"1"}),"instanceName":"1"}),"instanceName":"1"}),"instanceName":"1"}),"instanceName":"1"});
            var Q1904;
            Q1904=makeQuery(id+"F13.opPattern","COPY",BODY,{"derivedFrom":makeQuery(id+"F10.opPattern","COPY",BODY,{"derivedFrom":makeQuery(id+"F9.opPattern","COPY",BODY,{"derivedFrom":makeQuery(id+"F8.opPattern","COPY",BODY,{"derivedFrom":makeQuery(id+"F7.opPattern","COPY",BODY,{"derivedFrom":makeQuery(id+"F5.opPattern","COPY",BODY,{"derivedFrom":makeQuery(id+"F4.opPattern","COPY",BODY,{"derivedFrom":makeQuery(id+"F1.opRevolve","SWEPT_BODY",BODY,{"disambiguationData":[OSD([sQuery(id+"F0.wireOp",EDGE,"E1")])]}),"instanceName":"1"}),"instanceName":"1"}),"instanceName":"1"}),"instanceName":"1"}),"instanceName":"1"}),"instanceName":"1"}),"instanceName":"1"});
            var Q1905;
            Q1905=makeQuery(id+"F13.opPattern","COPY",BODY,{"derivedFrom":makeQuery(id+"F10.opPattern","COPY",BODY,{"derivedFrom":makeQuery(id+"F9.opPattern","COPY",BODY,{"derivedFrom":makeQuery(id+"F8.opPattern","COPY",BODY,{"derivedFrom":makeQuery(id+"F7.opPattern","COPY",BODY,{"derivedFrom":makeQuery(id+"F5.opPattern","COPY",BODY,{"derivedFrom":makeQuery(id+"F4.opPattern","COPY",BODY,{"derivedFrom":makeQuery(id+"F2.opPattern","COPY",BODY,{"derivedFrom":makeQuery(id+"F1.opRevolve","SWEPT_BODY",BODY,{"disambiguationData":[OSD([sQuery(id+"F0.wireOp",EDGE,"E1")])]}),"instanceName":"1"}),"instanceName":"1"}),"instanceName":"1"}),"instanceName":"1"}),"instanceName":"1"}),"instanceName":"1"}),"instanceName":"1"}),"instanceName":"1"});
            var Q1906;
            Q1906=makeQuery(id+"F13.opPattern","COPY",BODY,{"derivedFrom":makeQuery(id+"F10.opPattern","COPY",BODY,{"derivedFrom":makeQuery(id+"F9.opPattern","COPY",BODY,{"derivedFrom":makeQuery(id+"F8.opPattern","COPY",BODY,{"derivedFrom":makeQuery(id+"F7.opPattern","COPY",BODY,{"derivedFrom":makeQuery(id+"F5.opPattern","COPY",BODY,{"derivedFrom":makeQuery(id+"F4.opPattern","COPY",BODY,{"derivedFrom":makeQuery(id+"F3.opPattern","COPY",BODY,{"derivedFrom":makeQuery(id+"F2.opPattern","COPY",BODY,{"derivedFrom":makeQuery(id+"F1.opRevolve","SWEPT_BODY",BODY,{"disambiguationData":[OSD([sQuery(id+"F0.wireOp",EDGE,"E1")])]}),"instanceName":"1"}),"instanceName":"1"}),"instanceName":"1"}),"instanceName":"1"}),"instanceName":"1"}),"instanceName":"1"}),"instanceName":"1"}),"instanceName":"1"}),"instanceName":"1"});
            var Q1907;
            Q1907=makeQuery(id+"F13.opPattern","COPY",BODY,{"derivedFrom":makeQuery(id+"F10.opPattern","COPY",BODY,{"derivedFrom":makeQuery(id+"F9.opPattern","COPY",BODY,{"derivedFrom":makeQuery(id+"F8.opPattern","COPY",BODY,{"derivedFrom":makeQuery(id+"F7.opPattern","COPY",BODY,{"derivedFrom":makeQuery(id+"F6.opPattern","COPY",BODY,{"derivedFrom":makeQuery(id+"F1.opRevolve","SWEPT_BODY",BODY,{"disambiguationData":[OSD([sQuery(id+"F0.wireOp",EDGE,"E1")])]}),"instanceName":"1"}),"instanceName":"1"}),"instanceName":"1"}),"instanceName":"1"}),"instanceName":"1"}),"instanceName":"1"});
            var Q1908;
            Q1908=makeQuery(id+"F13.opPattern","COPY",BODY,{"derivedFrom":makeQuery(id+"F10.opPattern","COPY",BODY,{"derivedFrom":makeQuery(id+"F9.opPattern","COPY",BODY,{"derivedFrom":makeQuery(id+"F8.opPattern","COPY",BODY,{"derivedFrom":makeQuery(id+"F7.opPattern","COPY",BODY,{"derivedFrom":makeQuery(id+"F6.opPattern","COPY",BODY,{"derivedFrom":makeQuery(id+"F2.opPattern","COPY",BODY,{"derivedFrom":makeQuery(id+"F1.opRevolve","SWEPT_BODY",BODY,{"disambiguationData":[OSD([sQuery(id+"F0.wireOp",EDGE,"E1")])]}),"instanceName":"1"}),"instanceName":"1"}),"instanceName":"1"}),"instanceName":"1"}),"instanceName":"1"}),"instanceName":"1"}),"instanceName":"1"});
            var Q1909;
            Q1909=makeQuery(id+"F13.opPattern","COPY",BODY,{"derivedFrom":makeQuery(id+"F10.opPattern","COPY",BODY,{"derivedFrom":makeQuery(id+"F9.opPattern","COPY",BODY,{"derivedFrom":makeQuery(id+"F8.opPattern","COPY",BODY,{"derivedFrom":makeQuery(id+"F7.opPattern","COPY",BODY,{"derivedFrom":makeQuery(id+"F6.opPattern","COPY",BODY,{"derivedFrom":makeQuery(id+"F3.opPattern","COPY",BODY,{"derivedFrom":makeQuery(id+"F2.opPattern","COPY",BODY,{"derivedFrom":makeQuery(id+"F1.opRevolve","SWEPT_BODY",BODY,{"disambiguationData":[OSD([sQuery(id+"F0.wireOp",EDGE,"E1")])]}),"instanceName":"1"}),"instanceName":"1"}),"instanceName":"1"}),"instanceName":"1"}),"instanceName":"1"}),"instanceName":"1"}),"instanceName":"1"}),"instanceName":"1"});
            var Q1910;
            Q1910=makeQuery(id+"F13.opPattern","COPY",BODY,{"derivedFrom":makeQuery(id+"F10.opPattern","COPY",BODY,{"derivedFrom":makeQuery(id+"F9.opPattern","COPY",BODY,{"derivedFrom":makeQuery(id+"F8.opPattern","COPY",BODY,{"derivedFrom":makeQuery(id+"F7.opPattern","COPY",BODY,{"derivedFrom":makeQuery(id+"F6.opPattern","COPY",BODY,{"derivedFrom":makeQuery(id+"F4.opPattern","COPY",BODY,{"derivedFrom":makeQuery(id+"F1.opRevolve","SWEPT_BODY",BODY,{"disambiguationData":[OSD([sQuery(id+"F0.wireOp",EDGE,"E1")])]}),"instanceName":"1"}),"instanceName":"1"}),"instanceName":"1"}),"instanceName":"1"}),"instanceName":"1"}),"instanceName":"1"}),"instanceName":"1"});
            var Q1911;
            Q1911=makeQuery(id+"F13.opPattern","COPY",BODY,{"derivedFrom":makeQuery(id+"F10.opPattern","COPY",BODY,{"derivedFrom":makeQuery(id+"F9.opPattern","COPY",BODY,{"derivedFrom":makeQuery(id+"F8.opPattern","COPY",BODY,{"derivedFrom":makeQuery(id+"F7.opPattern","COPY",BODY,{"derivedFrom":makeQuery(id+"F6.opPattern","COPY",BODY,{"derivedFrom":makeQuery(id+"F4.opPattern","COPY",BODY,{"derivedFrom":makeQuery(id+"F2.opPattern","COPY",BODY,{"derivedFrom":makeQuery(id+"F1.opRevolve","SWEPT_BODY",BODY,{"disambiguationData":[OSD([sQuery(id+"F0.wireOp",EDGE,"E1")])]}),"instanceName":"1"}),"instanceName":"1"}),"instanceName":"1"}),"instanceName":"1"}),"instanceName":"1"}),"instanceName":"1"}),"instanceName":"1"}),"instanceName":"1"});
            var Q1912;
            Q1912=makeQuery(id+"F13.opPattern","COPY",BODY,{"derivedFrom":makeQuery(id+"F10.opPattern","COPY",BODY,{"derivedFrom":makeQuery(id+"F9.opPattern","COPY",BODY,{"derivedFrom":makeQuery(id+"F8.opPattern","COPY",BODY,{"derivedFrom":makeQuery(id+"F7.opPattern","COPY",BODY,{"derivedFrom":makeQuery(id+"F6.opPattern","COPY",BODY,{"derivedFrom":makeQuery(id+"F4.opPattern","COPY",BODY,{"derivedFrom":makeQuery(id+"F3.opPattern","COPY",BODY,{"derivedFrom":makeQuery(id+"F2.opPattern","COPY",BODY,{"derivedFrom":makeQuery(id+"F1.opRevolve","SWEPT_BODY",BODY,{"disambiguationData":[OSD([sQuery(id+"F0.wireOp",EDGE,"E1")])]}),"instanceName":"1"}),"instanceName":"1"}),"instanceName":"1"}),"instanceName":"1"}),"instanceName":"1"}),"instanceName":"1"}),"instanceName":"1"}),"instanceName":"1"}),"instanceName":"1"});
            var Q1913;
            Q1913=makeQuery(id+"F13.opPattern","COPY",BODY,{"derivedFrom":makeQuery(id+"F10.opPattern","COPY",BODY,{"derivedFrom":makeQuery(id+"F9.opPattern","COPY",BODY,{"derivedFrom":makeQuery(id+"F8.opPattern","COPY",BODY,{"derivedFrom":makeQuery(id+"F7.opPattern","COPY",BODY,{"derivedFrom":makeQuery(id+"F6.opPattern","COPY",BODY,{"derivedFrom":makeQuery(id+"F5.opPattern","COPY",BODY,{"derivedFrom":makeQuery(id+"F1.opRevolve","SWEPT_BODY",BODY,{"disambiguationData":[OSD([sQuery(id+"F0.wireOp",EDGE,"E1")])]}),"instanceName":"1"}),"instanceName":"1"}),"instanceName":"1"}),"instanceName":"1"}),"instanceName":"1"}),"instanceName":"1"}),"instanceName":"1"});
            var Q1914;
            Q1914=makeQuery(id+"F13.opPattern","COPY",BODY,{"derivedFrom":makeQuery(id+"F10.opPattern","COPY",BODY,{"derivedFrom":makeQuery(id+"F9.opPattern","COPY",BODY,{"derivedFrom":makeQuery(id+"F8.opPattern","COPY",BODY,{"derivedFrom":makeQuery(id+"F7.opPattern","COPY",BODY,{"derivedFrom":makeQuery(id+"F6.opPattern","COPY",BODY,{"derivedFrom":makeQuery(id+"F5.opPattern","COPY",BODY,{"derivedFrom":makeQuery(id+"F2.opPattern","COPY",BODY,{"derivedFrom":makeQuery(id+"F1.opRevolve","SWEPT_BODY",BODY,{"disambiguationData":[OSD([sQuery(id+"F0.wireOp",EDGE,"E1")])]}),"instanceName":"1"}),"instanceName":"1"}),"instanceName":"1"}),"instanceName":"1"}),"instanceName":"1"}),"instanceName":"1"}),"instanceName":"1"}),"instanceName":"1"});
            var Q1915;
            Q1915=makeQuery(id+"F13.opPattern","COPY",BODY,{"derivedFrom":makeQuery(id+"F10.opPattern","COPY",BODY,{"derivedFrom":makeQuery(id+"F9.opPattern","COPY",BODY,{"derivedFrom":makeQuery(id+"F8.opPattern","COPY",BODY,{"derivedFrom":makeQuery(id+"F7.opPattern","COPY",BODY,{"derivedFrom":makeQuery(id+"F6.opPattern","COPY",BODY,{"derivedFrom":makeQuery(id+"F5.opPattern","COPY",BODY,{"derivedFrom":makeQuery(id+"F3.opPattern","COPY",BODY,{"derivedFrom":makeQuery(id+"F2.opPattern","COPY",BODY,{"derivedFrom":makeQuery(id+"F1.opRevolve","SWEPT_BODY",BODY,{"disambiguationData":[OSD([sQuery(id+"F0.wireOp",EDGE,"E1")])]}),"instanceName":"1"}),"instanceName":"1"}),"instanceName":"1"}),"instanceName":"1"}),"instanceName":"1"}),"instanceName":"1"}),"instanceName":"1"}),"instanceName":"1"}),"instanceName":"1"});
            var Q1916;
            Q1916=makeQuery(id+"F13.opPattern","COPY",BODY,{"derivedFrom":makeQuery(id+"F10.opPattern","COPY",BODY,{"derivedFrom":makeQuery(id+"F9.opPattern","COPY",BODY,{"derivedFrom":makeQuery(id+"F8.opPattern","COPY",BODY,{"derivedFrom":makeQuery(id+"F7.opPattern","COPY",BODY,{"derivedFrom":makeQuery(id+"F6.opPattern","COPY",BODY,{"derivedFrom":makeQuery(id+"F5.opPattern","COPY",BODY,{"derivedFrom":makeQuery(id+"F4.opPattern","COPY",BODY,{"derivedFrom":makeQuery(id+"F1.opRevolve","SWEPT_BODY",BODY,{"disambiguationData":[OSD([sQuery(id+"F0.wireOp",EDGE,"E1")])]}),"instanceName":"1"}),"instanceName":"1"}),"instanceName":"1"}),"instanceName":"1"}),"instanceName":"1"}),"instanceName":"1"}),"instanceName":"1"}),"instanceName":"1"});
            var Q1917;
            Q1917=makeQuery(id+"F13.opPattern","COPY",BODY,{"derivedFrom":makeQuery(id+"F10.opPattern","COPY",BODY,{"derivedFrom":makeQuery(id+"F9.opPattern","COPY",BODY,{"derivedFrom":makeQuery(id+"F8.opPattern","COPY",BODY,{"derivedFrom":makeQuery(id+"F7.opPattern","COPY",BODY,{"derivedFrom":makeQuery(id+"F6.opPattern","COPY",BODY,{"derivedFrom":makeQuery(id+"F5.opPattern","COPY",BODY,{"derivedFrom":makeQuery(id+"F4.opPattern","COPY",BODY,{"derivedFrom":makeQuery(id+"F2.opPattern","COPY",BODY,{"derivedFrom":makeQuery(id+"F1.opRevolve","SWEPT_BODY",BODY,{"disambiguationData":[OSD([sQuery(id+"F0.wireOp",EDGE,"E1")])]}),"instanceName":"1"}),"instanceName":"1"}),"instanceName":"1"}),"instanceName":"1"}),"instanceName":"1"}),"instanceName":"1"}),"instanceName":"1"}),"instanceName":"1"}),"instanceName":"1"});
            var Q1918;
            Q1918=makeQuery(id+"F13.opPattern","COPY",BODY,{"derivedFrom":makeQuery(id+"F10.opPattern","COPY",BODY,{"derivedFrom":makeQuery(id+"F9.opPattern","COPY",BODY,{"derivedFrom":makeQuery(id+"F8.opPattern","COPY",BODY,{"derivedFrom":makeQuery(id+"F7.opPattern","COPY",BODY,{"derivedFrom":makeQuery(id+"F6.opPattern","COPY",BODY,{"derivedFrom":makeQuery(id+"F5.opPattern","COPY",BODY,{"derivedFrom":makeQuery(id+"F4.opPattern","COPY",BODY,{"derivedFrom":makeQuery(id+"F3.opPattern","COPY",BODY,{"derivedFrom":makeQuery(id+"F2.opPattern","COPY",BODY,{"derivedFrom":makeQuery(id+"F1.opRevolve","SWEPT_BODY",BODY,{"disambiguationData":[OSD([sQuery(id+"F0.wireOp",EDGE,"E1")])]}),"instanceName":"1"}),"instanceName":"1"}),"instanceName":"1"}),"instanceName":"1"}),"instanceName":"1"}),"instanceName":"1"}),"instanceName":"1"}),"instanceName":"1"}),"instanceName":"1"}),"instanceName":"1"});
            var Q1919;
            Q1919=makeQuery(id+"F13.opPattern","COPY",BODY,{"derivedFrom":makeQuery(id+"F11.opPattern","COPY",BODY,{"derivedFrom":makeQuery(id+"F1.opRevolve","SWEPT_BODY",BODY,{"disambiguationData":[OSD([sQuery(id+"F0.wireOp",EDGE,"E1")])]}),"instanceName":"1"}),"instanceName":"1"});
            var Q1920;
            Q1920=makeQuery(id+"F13.opPattern","COPY",BODY,{"derivedFrom":makeQuery(id+"F11.opPattern","COPY",BODY,{"derivedFrom":makeQuery(id+"F2.opPattern","COPY",BODY,{"derivedFrom":makeQuery(id+"F1.opRevolve","SWEPT_BODY",BODY,{"disambiguationData":[OSD([sQuery(id+"F0.wireOp",EDGE,"E1")])]}),"instanceName":"1"}),"instanceName":"1"}),"instanceName":"1"});
            var Q1921;
            Q1921=makeQuery(id+"F13.opPattern","COPY",BODY,{"derivedFrom":makeQuery(id+"F11.opPattern","COPY",BODY,{"derivedFrom":makeQuery(id+"F3.opPattern","COPY",BODY,{"derivedFrom":makeQuery(id+"F2.opPattern","COPY",BODY,{"derivedFrom":makeQuery(id+"F1.opRevolve","SWEPT_BODY",BODY,{"disambiguationData":[OSD([sQuery(id+"F0.wireOp",EDGE,"E1")])]}),"instanceName":"1"}),"instanceName":"1"}),"instanceName":"1"}),"instanceName":"1"});
            var Q1922;
            Q1922=makeQuery(id+"F13.opPattern","COPY",BODY,{"derivedFrom":makeQuery(id+"F11.opPattern","COPY",BODY,{"derivedFrom":makeQuery(id+"F4.opPattern","COPY",BODY,{"derivedFrom":makeQuery(id+"F1.opRevolve","SWEPT_BODY",BODY,{"disambiguationData":[OSD([sQuery(id+"F0.wireOp",EDGE,"E1")])]}),"instanceName":"1"}),"instanceName":"1"}),"instanceName":"1"});
            var Q1923;
            Q1923=makeQuery(id+"F13.opPattern","COPY",BODY,{"derivedFrom":makeQuery(id+"F11.opPattern","COPY",BODY,{"derivedFrom":makeQuery(id+"F4.opPattern","COPY",BODY,{"derivedFrom":makeQuery(id+"F2.opPattern","COPY",BODY,{"derivedFrom":makeQuery(id+"F1.opRevolve","SWEPT_BODY",BODY,{"disambiguationData":[OSD([sQuery(id+"F0.wireOp",EDGE,"E1")])]}),"instanceName":"1"}),"instanceName":"1"}),"instanceName":"1"}),"instanceName":"1"});
            var Q1924;
            Q1924=makeQuery(id+"F13.opPattern","COPY",BODY,{"derivedFrom":makeQuery(id+"F11.opPattern","COPY",BODY,{"derivedFrom":makeQuery(id+"F4.opPattern","COPY",BODY,{"derivedFrom":makeQuery(id+"F3.opPattern","COPY",BODY,{"derivedFrom":makeQuery(id+"F2.opPattern","COPY",BODY,{"derivedFrom":makeQuery(id+"F1.opRevolve","SWEPT_BODY",BODY,{"disambiguationData":[OSD([sQuery(id+"F0.wireOp",EDGE,"E1")])]}),"instanceName":"1"}),"instanceName":"1"}),"instanceName":"1"}),"instanceName":"1"}),"instanceName":"1"});
            var Q1925;
            Q1925=makeQuery(id+"F13.opPattern","COPY",BODY,{"derivedFrom":makeQuery(id+"F11.opPattern","COPY",BODY,{"derivedFrom":makeQuery(id+"F5.opPattern","COPY",BODY,{"derivedFrom":makeQuery(id+"F1.opRevolve","SWEPT_BODY",BODY,{"disambiguationData":[OSD([sQuery(id+"F0.wireOp",EDGE,"E1")])]}),"instanceName":"1"}),"instanceName":"1"}),"instanceName":"1"});
            var Q1926;
            Q1926=makeQuery(id+"F13.opPattern","COPY",BODY,{"derivedFrom":makeQuery(id+"F11.opPattern","COPY",BODY,{"derivedFrom":makeQuery(id+"F5.opPattern","COPY",BODY,{"derivedFrom":makeQuery(id+"F2.opPattern","COPY",BODY,{"derivedFrom":makeQuery(id+"F1.opRevolve","SWEPT_BODY",BODY,{"disambiguationData":[OSD([sQuery(id+"F0.wireOp",EDGE,"E1")])]}),"instanceName":"1"}),"instanceName":"1"}),"instanceName":"1"}),"instanceName":"1"});
            var Q1927;
            Q1927=makeQuery(id+"F13.opPattern","COPY",BODY,{"derivedFrom":makeQuery(id+"F11.opPattern","COPY",BODY,{"derivedFrom":makeQuery(id+"F5.opPattern","COPY",BODY,{"derivedFrom":makeQuery(id+"F3.opPattern","COPY",BODY,{"derivedFrom":makeQuery(id+"F2.opPattern","COPY",BODY,{"derivedFrom":makeQuery(id+"F1.opRevolve","SWEPT_BODY",BODY,{"disambiguationData":[OSD([sQuery(id+"F0.wireOp",EDGE,"E1")])]}),"instanceName":"1"}),"instanceName":"1"}),"instanceName":"1"}),"instanceName":"1"}),"instanceName":"1"});
            var Q1928;
            Q1928=makeQuery(id+"F13.opPattern","COPY",BODY,{"derivedFrom":makeQuery(id+"F11.opPattern","COPY",BODY,{"derivedFrom":makeQuery(id+"F5.opPattern","COPY",BODY,{"derivedFrom":makeQuery(id+"F4.opPattern","COPY",BODY,{"derivedFrom":makeQuery(id+"F1.opRevolve","SWEPT_BODY",BODY,{"disambiguationData":[OSD([sQuery(id+"F0.wireOp",EDGE,"E1")])]}),"instanceName":"1"}),"instanceName":"1"}),"instanceName":"1"}),"instanceName":"1"});
            var Q1929;
            Q1929=makeQuery(id+"F13.opPattern","COPY",BODY,{"derivedFrom":makeQuery(id+"F11.opPattern","COPY",BODY,{"derivedFrom":makeQuery(id+"F5.opPattern","COPY",BODY,{"derivedFrom":makeQuery(id+"F4.opPattern","COPY",BODY,{"derivedFrom":makeQuery(id+"F2.opPattern","COPY",BODY,{"derivedFrom":makeQuery(id+"F1.opRevolve","SWEPT_BODY",BODY,{"disambiguationData":[OSD([sQuery(id+"F0.wireOp",EDGE,"E1")])]}),"instanceName":"1"}),"instanceName":"1"}),"instanceName":"1"}),"instanceName":"1"}),"instanceName":"1"});
            var Q1930;
            Q1930=makeQuery(id+"F13.opPattern","COPY",BODY,{"derivedFrom":makeQuery(id+"F11.opPattern","COPY",BODY,{"derivedFrom":makeQuery(id+"F5.opPattern","COPY",BODY,{"derivedFrom":makeQuery(id+"F4.opPattern","COPY",BODY,{"derivedFrom":makeQuery(id+"F3.opPattern","COPY",BODY,{"derivedFrom":makeQuery(id+"F2.opPattern","COPY",BODY,{"derivedFrom":makeQuery(id+"F1.opRevolve","SWEPT_BODY",BODY,{"disambiguationData":[OSD([sQuery(id+"F0.wireOp",EDGE,"E1")])]}),"instanceName":"1"}),"instanceName":"1"}),"instanceName":"1"}),"instanceName":"1"}),"instanceName":"1"}),"instanceName":"1"});
            var Q1931;
            Q1931=makeQuery(id+"F13.opPattern","COPY",BODY,{"derivedFrom":makeQuery(id+"F11.opPattern","COPY",BODY,{"derivedFrom":makeQuery(id+"F6.opPattern","COPY",BODY,{"derivedFrom":makeQuery(id+"F1.opRevolve","SWEPT_BODY",BODY,{"disambiguationData":[OSD([sQuery(id+"F0.wireOp",EDGE,"E1")])]}),"instanceName":"1"}),"instanceName":"1"}),"instanceName":"1"});
            var Q1932;
            Q1932=makeQuery(id+"F13.opPattern","COPY",BODY,{"derivedFrom":makeQuery(id+"F11.opPattern","COPY",BODY,{"derivedFrom":makeQuery(id+"F6.opPattern","COPY",BODY,{"derivedFrom":makeQuery(id+"F2.opPattern","COPY",BODY,{"derivedFrom":makeQuery(id+"F1.opRevolve","SWEPT_BODY",BODY,{"disambiguationData":[OSD([sQuery(id+"F0.wireOp",EDGE,"E1")])]}),"instanceName":"1"}),"instanceName":"1"}),"instanceName":"1"}),"instanceName":"1"});
            var Q1933;
            Q1933=makeQuery(id+"F13.opPattern","COPY",BODY,{"derivedFrom":makeQuery(id+"F11.opPattern","COPY",BODY,{"derivedFrom":makeQuery(id+"F6.opPattern","COPY",BODY,{"derivedFrom":makeQuery(id+"F3.opPattern","COPY",BODY,{"derivedFrom":makeQuery(id+"F2.opPattern","COPY",BODY,{"derivedFrom":makeQuery(id+"F1.opRevolve","SWEPT_BODY",BODY,{"disambiguationData":[OSD([sQuery(id+"F0.wireOp",EDGE,"E1")])]}),"instanceName":"1"}),"instanceName":"1"}),"instanceName":"1"}),"instanceName":"1"}),"instanceName":"1"});
            var Q1934;
            Q1934=makeQuery(id+"F13.opPattern","COPY",BODY,{"derivedFrom":makeQuery(id+"F11.opPattern","COPY",BODY,{"derivedFrom":makeQuery(id+"F6.opPattern","COPY",BODY,{"derivedFrom":makeQuery(id+"F4.opPattern","COPY",BODY,{"derivedFrom":makeQuery(id+"F1.opRevolve","SWEPT_BODY",BODY,{"disambiguationData":[OSD([sQuery(id+"F0.wireOp",EDGE,"E1")])]}),"instanceName":"1"}),"instanceName":"1"}),"instanceName":"1"}),"instanceName":"1"});
            var Q1935;
            Q1935=makeQuery(id+"F13.opPattern","COPY",BODY,{"derivedFrom":makeQuery(id+"F11.opPattern","COPY",BODY,{"derivedFrom":makeQuery(id+"F6.opPattern","COPY",BODY,{"derivedFrom":makeQuery(id+"F4.opPattern","COPY",BODY,{"derivedFrom":makeQuery(id+"F2.opPattern","COPY",BODY,{"derivedFrom":makeQuery(id+"F1.opRevolve","SWEPT_BODY",BODY,{"disambiguationData":[OSD([sQuery(id+"F0.wireOp",EDGE,"E1")])]}),"instanceName":"1"}),"instanceName":"1"}),"instanceName":"1"}),"instanceName":"1"}),"instanceName":"1"});
            var Q1936;
            Q1936=makeQuery(id+"F13.opPattern","COPY",BODY,{"derivedFrom":makeQuery(id+"F11.opPattern","COPY",BODY,{"derivedFrom":makeQuery(id+"F6.opPattern","COPY",BODY,{"derivedFrom":makeQuery(id+"F4.opPattern","COPY",BODY,{"derivedFrom":makeQuery(id+"F3.opPattern","COPY",BODY,{"derivedFrom":makeQuery(id+"F2.opPattern","COPY",BODY,{"derivedFrom":makeQuery(id+"F1.opRevolve","SWEPT_BODY",BODY,{"disambiguationData":[OSD([sQuery(id+"F0.wireOp",EDGE,"E1")])]}),"instanceName":"1"}),"instanceName":"1"}),"instanceName":"1"}),"instanceName":"1"}),"instanceName":"1"}),"instanceName":"1"});
            var Q1937;
            Q1937=makeQuery(id+"F13.opPattern","COPY",BODY,{"derivedFrom":makeQuery(id+"F11.opPattern","COPY",BODY,{"derivedFrom":makeQuery(id+"F6.opPattern","COPY",BODY,{"derivedFrom":makeQuery(id+"F5.opPattern","COPY",BODY,{"derivedFrom":makeQuery(id+"F1.opRevolve","SWEPT_BODY",BODY,{"disambiguationData":[OSD([sQuery(id+"F0.wireOp",EDGE,"E1")])]}),"instanceName":"1"}),"instanceName":"1"}),"instanceName":"1"}),"instanceName":"1"});
            var Q1938;
            Q1938=makeQuery(id+"F13.opPattern","COPY",BODY,{"derivedFrom":makeQuery(id+"F11.opPattern","COPY",BODY,{"derivedFrom":makeQuery(id+"F6.opPattern","COPY",BODY,{"derivedFrom":makeQuery(id+"F5.opPattern","COPY",BODY,{"derivedFrom":makeQuery(id+"F2.opPattern","COPY",BODY,{"derivedFrom":makeQuery(id+"F1.opRevolve","SWEPT_BODY",BODY,{"disambiguationData":[OSD([sQuery(id+"F0.wireOp",EDGE,"E1")])]}),"instanceName":"1"}),"instanceName":"1"}),"instanceName":"1"}),"instanceName":"1"}),"instanceName":"1"});
            var Q1939;
            Q1939=makeQuery(id+"F13.opPattern","COPY",BODY,{"derivedFrom":makeQuery(id+"F11.opPattern","COPY",BODY,{"derivedFrom":makeQuery(id+"F6.opPattern","COPY",BODY,{"derivedFrom":makeQuery(id+"F5.opPattern","COPY",BODY,{"derivedFrom":makeQuery(id+"F3.opPattern","COPY",BODY,{"derivedFrom":makeQuery(id+"F2.opPattern","COPY",BODY,{"derivedFrom":makeQuery(id+"F1.opRevolve","SWEPT_BODY",BODY,{"disambiguationData":[OSD([sQuery(id+"F0.wireOp",EDGE,"E1")])]}),"instanceName":"1"}),"instanceName":"1"}),"instanceName":"1"}),"instanceName":"1"}),"instanceName":"1"}),"instanceName":"1"});
            var Q1940;
            Q1940=makeQuery(id+"F13.opPattern","COPY",BODY,{"derivedFrom":makeQuery(id+"F11.opPattern","COPY",BODY,{"derivedFrom":makeQuery(id+"F6.opPattern","COPY",BODY,{"derivedFrom":makeQuery(id+"F5.opPattern","COPY",BODY,{"derivedFrom":makeQuery(id+"F4.opPattern","COPY",BODY,{"derivedFrom":makeQuery(id+"F1.opRevolve","SWEPT_BODY",BODY,{"disambiguationData":[OSD([sQuery(id+"F0.wireOp",EDGE,"E1")])]}),"instanceName":"1"}),"instanceName":"1"}),"instanceName":"1"}),"instanceName":"1"}),"instanceName":"1"});
            var Q1941;
            Q1941=makeQuery(id+"F13.opPattern","COPY",BODY,{"derivedFrom":makeQuery(id+"F11.opPattern","COPY",BODY,{"derivedFrom":makeQuery(id+"F6.opPattern","COPY",BODY,{"derivedFrom":makeQuery(id+"F5.opPattern","COPY",BODY,{"derivedFrom":makeQuery(id+"F4.opPattern","COPY",BODY,{"derivedFrom":makeQuery(id+"F2.opPattern","COPY",BODY,{"derivedFrom":makeQuery(id+"F1.opRevolve","SWEPT_BODY",BODY,{"disambiguationData":[OSD([sQuery(id+"F0.wireOp",EDGE,"E1")])]}),"instanceName":"1"}),"instanceName":"1"}),"instanceName":"1"}),"instanceName":"1"}),"instanceName":"1"}),"instanceName":"1"});
            var Q1942;
            Q1942=makeQuery(id+"F13.opPattern","COPY",BODY,{"derivedFrom":makeQuery(id+"F11.opPattern","COPY",BODY,{"derivedFrom":makeQuery(id+"F6.opPattern","COPY",BODY,{"derivedFrom":makeQuery(id+"F5.opPattern","COPY",BODY,{"derivedFrom":makeQuery(id+"F4.opPattern","COPY",BODY,{"derivedFrom":makeQuery(id+"F3.opPattern","COPY",BODY,{"derivedFrom":makeQuery(id+"F2.opPattern","COPY",BODY,{"derivedFrom":makeQuery(id+"F1.opRevolve","SWEPT_BODY",BODY,{"disambiguationData":[OSD([sQuery(id+"F0.wireOp",EDGE,"E1")])]}),"instanceName":"1"}),"instanceName":"1"}),"instanceName":"1"}),"instanceName":"1"}),"instanceName":"1"}),"instanceName":"1"}),"instanceName":"1"});
            var Q1943;
            Q1943=makeQuery(id+"F13.opPattern","COPY",BODY,{"derivedFrom":makeQuery(id+"F11.opPattern","COPY",BODY,{"derivedFrom":makeQuery(id+"F7.opPattern","COPY",BODY,{"derivedFrom":makeQuery(id+"F1.opRevolve","SWEPT_BODY",BODY,{"disambiguationData":[OSD([sQuery(id+"F0.wireOp",EDGE,"E1")])]}),"instanceName":"1"}),"instanceName":"1"}),"instanceName":"1"});
            var Q1944;
            Q1944=makeQuery(id+"F13.opPattern","COPY",BODY,{"derivedFrom":makeQuery(id+"F11.opPattern","COPY",BODY,{"derivedFrom":makeQuery(id+"F7.opPattern","COPY",BODY,{"derivedFrom":makeQuery(id+"F2.opPattern","COPY",BODY,{"derivedFrom":makeQuery(id+"F1.opRevolve","SWEPT_BODY",BODY,{"disambiguationData":[OSD([sQuery(id+"F0.wireOp",EDGE,"E1")])]}),"instanceName":"1"}),"instanceName":"1"}),"instanceName":"1"}),"instanceName":"1"});
            var Q1945;
            Q1945=makeQuery(id+"F13.opPattern","COPY",BODY,{"derivedFrom":makeQuery(id+"F11.opPattern","COPY",BODY,{"derivedFrom":makeQuery(id+"F7.opPattern","COPY",BODY,{"derivedFrom":makeQuery(id+"F3.opPattern","COPY",BODY,{"derivedFrom":makeQuery(id+"F2.opPattern","COPY",BODY,{"derivedFrom":makeQuery(id+"F1.opRevolve","SWEPT_BODY",BODY,{"disambiguationData":[OSD([sQuery(id+"F0.wireOp",EDGE,"E1")])]}),"instanceName":"1"}),"instanceName":"1"}),"instanceName":"1"}),"instanceName":"1"}),"instanceName":"1"});
            var Q1946;
            Q1946=makeQuery(id+"F13.opPattern","COPY",BODY,{"derivedFrom":makeQuery(id+"F11.opPattern","COPY",BODY,{"derivedFrom":makeQuery(id+"F7.opPattern","COPY",BODY,{"derivedFrom":makeQuery(id+"F4.opPattern","COPY",BODY,{"derivedFrom":makeQuery(id+"F1.opRevolve","SWEPT_BODY",BODY,{"disambiguationData":[OSD([sQuery(id+"F0.wireOp",EDGE,"E1")])]}),"instanceName":"1"}),"instanceName":"1"}),"instanceName":"1"}),"instanceName":"1"});
            var Q1947;
            Q1947=makeQuery(id+"F13.opPattern","COPY",BODY,{"derivedFrom":makeQuery(id+"F11.opPattern","COPY",BODY,{"derivedFrom":makeQuery(id+"F7.opPattern","COPY",BODY,{"derivedFrom":makeQuery(id+"F4.opPattern","COPY",BODY,{"derivedFrom":makeQuery(id+"F2.opPattern","COPY",BODY,{"derivedFrom":makeQuery(id+"F1.opRevolve","SWEPT_BODY",BODY,{"disambiguationData":[OSD([sQuery(id+"F0.wireOp",EDGE,"E1")])]}),"instanceName":"1"}),"instanceName":"1"}),"instanceName":"1"}),"instanceName":"1"}),"instanceName":"1"});
            var Q1948;
            Q1948=makeQuery(id+"F13.opPattern","COPY",BODY,{"derivedFrom":makeQuery(id+"F11.opPattern","COPY",BODY,{"derivedFrom":makeQuery(id+"F7.opPattern","COPY",BODY,{"derivedFrom":makeQuery(id+"F4.opPattern","COPY",BODY,{"derivedFrom":makeQuery(id+"F3.opPattern","COPY",BODY,{"derivedFrom":makeQuery(id+"F2.opPattern","COPY",BODY,{"derivedFrom":makeQuery(id+"F1.opRevolve","SWEPT_BODY",BODY,{"disambiguationData":[OSD([sQuery(id+"F0.wireOp",EDGE,"E1")])]}),"instanceName":"1"}),"instanceName":"1"}),"instanceName":"1"}),"instanceName":"1"}),"instanceName":"1"}),"instanceName":"1"});
            var Q1949;
            Q1949=makeQuery(id+"F13.opPattern","COPY",BODY,{"derivedFrom":makeQuery(id+"F11.opPattern","COPY",BODY,{"derivedFrom":makeQuery(id+"F7.opPattern","COPY",BODY,{"derivedFrom":makeQuery(id+"F5.opPattern","COPY",BODY,{"derivedFrom":makeQuery(id+"F1.opRevolve","SWEPT_BODY",BODY,{"disambiguationData":[OSD([sQuery(id+"F0.wireOp",EDGE,"E1")])]}),"instanceName":"1"}),"instanceName":"1"}),"instanceName":"1"}),"instanceName":"1"});
            var Q1950;
            Q1950=makeQuery(id+"F13.opPattern","COPY",BODY,{"derivedFrom":makeQuery(id+"F11.opPattern","COPY",BODY,{"derivedFrom":makeQuery(id+"F7.opPattern","COPY",BODY,{"derivedFrom":makeQuery(id+"F5.opPattern","COPY",BODY,{"derivedFrom":makeQuery(id+"F2.opPattern","COPY",BODY,{"derivedFrom":makeQuery(id+"F1.opRevolve","SWEPT_BODY",BODY,{"disambiguationData":[OSD([sQuery(id+"F0.wireOp",EDGE,"E1")])]}),"instanceName":"1"}),"instanceName":"1"}),"instanceName":"1"}),"instanceName":"1"}),"instanceName":"1"});
            var Q1951;
            Q1951=makeQuery(id+"F13.opPattern","COPY",BODY,{"derivedFrom":makeQuery(id+"F11.opPattern","COPY",BODY,{"derivedFrom":makeQuery(id+"F7.opPattern","COPY",BODY,{"derivedFrom":makeQuery(id+"F5.opPattern","COPY",BODY,{"derivedFrom":makeQuery(id+"F3.opPattern","COPY",BODY,{"derivedFrom":makeQuery(id+"F2.opPattern","COPY",BODY,{"derivedFrom":makeQuery(id+"F1.opRevolve","SWEPT_BODY",BODY,{"disambiguationData":[OSD([sQuery(id+"F0.wireOp",EDGE,"E1")])]}),"instanceName":"1"}),"instanceName":"1"}),"instanceName":"1"}),"instanceName":"1"}),"instanceName":"1"}),"instanceName":"1"});
            var Q1952;
            Q1952=makeQuery(id+"F13.opPattern","COPY",BODY,{"derivedFrom":makeQuery(id+"F11.opPattern","COPY",BODY,{"derivedFrom":makeQuery(id+"F7.opPattern","COPY",BODY,{"derivedFrom":makeQuery(id+"F5.opPattern","COPY",BODY,{"derivedFrom":makeQuery(id+"F4.opPattern","COPY",BODY,{"derivedFrom":makeQuery(id+"F1.opRevolve","SWEPT_BODY",BODY,{"disambiguationData":[OSD([sQuery(id+"F0.wireOp",EDGE,"E1")])]}),"instanceName":"1"}),"instanceName":"1"}),"instanceName":"1"}),"instanceName":"1"}),"instanceName":"1"});
            var Q1953;
            Q1953=makeQuery(id+"F13.opPattern","COPY",BODY,{"derivedFrom":makeQuery(id+"F11.opPattern","COPY",BODY,{"derivedFrom":makeQuery(id+"F7.opPattern","COPY",BODY,{"derivedFrom":makeQuery(id+"F5.opPattern","COPY",BODY,{"derivedFrom":makeQuery(id+"F4.opPattern","COPY",BODY,{"derivedFrom":makeQuery(id+"F2.opPattern","COPY",BODY,{"derivedFrom":makeQuery(id+"F1.opRevolve","SWEPT_BODY",BODY,{"disambiguationData":[OSD([sQuery(id+"F0.wireOp",EDGE,"E1")])]}),"instanceName":"1"}),"instanceName":"1"}),"instanceName":"1"}),"instanceName":"1"}),"instanceName":"1"}),"instanceName":"1"});
            var Q1954;
            Q1954=makeQuery(id+"F13.opPattern","COPY",BODY,{"derivedFrom":makeQuery(id+"F11.opPattern","COPY",BODY,{"derivedFrom":makeQuery(id+"F7.opPattern","COPY",BODY,{"derivedFrom":makeQuery(id+"F5.opPattern","COPY",BODY,{"derivedFrom":makeQuery(id+"F4.opPattern","COPY",BODY,{"derivedFrom":makeQuery(id+"F3.opPattern","COPY",BODY,{"derivedFrom":makeQuery(id+"F2.opPattern","COPY",BODY,{"derivedFrom":makeQuery(id+"F1.opRevolve","SWEPT_BODY",BODY,{"disambiguationData":[OSD([sQuery(id+"F0.wireOp",EDGE,"E1")])]}),"instanceName":"1"}),"instanceName":"1"}),"instanceName":"1"}),"instanceName":"1"}),"instanceName":"1"}),"instanceName":"1"}),"instanceName":"1"});
            var Q1955;
            Q1955=makeQuery(id+"F13.opPattern","COPY",BODY,{"derivedFrom":makeQuery(id+"F11.opPattern","COPY",BODY,{"derivedFrom":makeQuery(id+"F7.opPattern","COPY",BODY,{"derivedFrom":makeQuery(id+"F6.opPattern","COPY",BODY,{"derivedFrom":makeQuery(id+"F1.opRevolve","SWEPT_BODY",BODY,{"disambiguationData":[OSD([sQuery(id+"F0.wireOp",EDGE,"E1")])]}),"instanceName":"1"}),"instanceName":"1"}),"instanceName":"1"}),"instanceName":"1"});
            var Q1956;
            Q1956=makeQuery(id+"F13.opPattern","COPY",BODY,{"derivedFrom":makeQuery(id+"F11.opPattern","COPY",BODY,{"derivedFrom":makeQuery(id+"F7.opPattern","COPY",BODY,{"derivedFrom":makeQuery(id+"F6.opPattern","COPY",BODY,{"derivedFrom":makeQuery(id+"F2.opPattern","COPY",BODY,{"derivedFrom":makeQuery(id+"F1.opRevolve","SWEPT_BODY",BODY,{"disambiguationData":[OSD([sQuery(id+"F0.wireOp",EDGE,"E1")])]}),"instanceName":"1"}),"instanceName":"1"}),"instanceName":"1"}),"instanceName":"1"}),"instanceName":"1"});
            var Q1957;
            Q1957=makeQuery(id+"F13.opPattern","COPY",BODY,{"derivedFrom":makeQuery(id+"F11.opPattern","COPY",BODY,{"derivedFrom":makeQuery(id+"F7.opPattern","COPY",BODY,{"derivedFrom":makeQuery(id+"F6.opPattern","COPY",BODY,{"derivedFrom":makeQuery(id+"F3.opPattern","COPY",BODY,{"derivedFrom":makeQuery(id+"F2.opPattern","COPY",BODY,{"derivedFrom":makeQuery(id+"F1.opRevolve","SWEPT_BODY",BODY,{"disambiguationData":[OSD([sQuery(id+"F0.wireOp",EDGE,"E1")])]}),"instanceName":"1"}),"instanceName":"1"}),"instanceName":"1"}),"instanceName":"1"}),"instanceName":"1"}),"instanceName":"1"});
            var Q1958;
            Q1958=makeQuery(id+"F13.opPattern","COPY",BODY,{"derivedFrom":makeQuery(id+"F11.opPattern","COPY",BODY,{"derivedFrom":makeQuery(id+"F7.opPattern","COPY",BODY,{"derivedFrom":makeQuery(id+"F6.opPattern","COPY",BODY,{"derivedFrom":makeQuery(id+"F4.opPattern","COPY",BODY,{"derivedFrom":makeQuery(id+"F1.opRevolve","SWEPT_BODY",BODY,{"disambiguationData":[OSD([sQuery(id+"F0.wireOp",EDGE,"E1")])]}),"instanceName":"1"}),"instanceName":"1"}),"instanceName":"1"}),"instanceName":"1"}),"instanceName":"1"});
            var Q1959;
            Q1959=makeQuery(id+"F13.opPattern","COPY",BODY,{"derivedFrom":makeQuery(id+"F11.opPattern","COPY",BODY,{"derivedFrom":makeQuery(id+"F7.opPattern","COPY",BODY,{"derivedFrom":makeQuery(id+"F6.opPattern","COPY",BODY,{"derivedFrom":makeQuery(id+"F4.opPattern","COPY",BODY,{"derivedFrom":makeQuery(id+"F2.opPattern","COPY",BODY,{"derivedFrom":makeQuery(id+"F1.opRevolve","SWEPT_BODY",BODY,{"disambiguationData":[OSD([sQuery(id+"F0.wireOp",EDGE,"E1")])]}),"instanceName":"1"}),"instanceName":"1"}),"instanceName":"1"}),"instanceName":"1"}),"instanceName":"1"}),"instanceName":"1"});
            var Q1960;
            Q1960=makeQuery(id+"F13.opPattern","COPY",BODY,{"derivedFrom":makeQuery(id+"F11.opPattern","COPY",BODY,{"derivedFrom":makeQuery(id+"F7.opPattern","COPY",BODY,{"derivedFrom":makeQuery(id+"F6.opPattern","COPY",BODY,{"derivedFrom":makeQuery(id+"F4.opPattern","COPY",BODY,{"derivedFrom":makeQuery(id+"F3.opPattern","COPY",BODY,{"derivedFrom":makeQuery(id+"F2.opPattern","COPY",BODY,{"derivedFrom":makeQuery(id+"F1.opRevolve","SWEPT_BODY",BODY,{"disambiguationData":[OSD([sQuery(id+"F0.wireOp",EDGE,"E1")])]}),"instanceName":"1"}),"instanceName":"1"}),"instanceName":"1"}),"instanceName":"1"}),"instanceName":"1"}),"instanceName":"1"}),"instanceName":"1"});
            var Q1961;
            Q1961=makeQuery(id+"F13.opPattern","COPY",BODY,{"derivedFrom":makeQuery(id+"F11.opPattern","COPY",BODY,{"derivedFrom":makeQuery(id+"F7.opPattern","COPY",BODY,{"derivedFrom":makeQuery(id+"F6.opPattern","COPY",BODY,{"derivedFrom":makeQuery(id+"F5.opPattern","COPY",BODY,{"derivedFrom":makeQuery(id+"F1.opRevolve","SWEPT_BODY",BODY,{"disambiguationData":[OSD([sQuery(id+"F0.wireOp",EDGE,"E1")])]}),"instanceName":"1"}),"instanceName":"1"}),"instanceName":"1"}),"instanceName":"1"}),"instanceName":"1"});
            var Q1962;
            Q1962=makeQuery(id+"F13.opPattern","COPY",BODY,{"derivedFrom":makeQuery(id+"F11.opPattern","COPY",BODY,{"derivedFrom":makeQuery(id+"F7.opPattern","COPY",BODY,{"derivedFrom":makeQuery(id+"F6.opPattern","COPY",BODY,{"derivedFrom":makeQuery(id+"F5.opPattern","COPY",BODY,{"derivedFrom":makeQuery(id+"F2.opPattern","COPY",BODY,{"derivedFrom":makeQuery(id+"F1.opRevolve","SWEPT_BODY",BODY,{"disambiguationData":[OSD([sQuery(id+"F0.wireOp",EDGE,"E1")])]}),"instanceName":"1"}),"instanceName":"1"}),"instanceName":"1"}),"instanceName":"1"}),"instanceName":"1"}),"instanceName":"1"});
            var Q1963;
            Q1963=makeQuery(id+"F13.opPattern","COPY",BODY,{"derivedFrom":makeQuery(id+"F11.opPattern","COPY",BODY,{"derivedFrom":makeQuery(id+"F7.opPattern","COPY",BODY,{"derivedFrom":makeQuery(id+"F6.opPattern","COPY",BODY,{"derivedFrom":makeQuery(id+"F5.opPattern","COPY",BODY,{"derivedFrom":makeQuery(id+"F3.opPattern","COPY",BODY,{"derivedFrom":makeQuery(id+"F2.opPattern","COPY",BODY,{"derivedFrom":makeQuery(id+"F1.opRevolve","SWEPT_BODY",BODY,{"disambiguationData":[OSD([sQuery(id+"F0.wireOp",EDGE,"E1")])]}),"instanceName":"1"}),"instanceName":"1"}),"instanceName":"1"}),"instanceName":"1"}),"instanceName":"1"}),"instanceName":"1"}),"instanceName":"1"});
            var Q1964;
            Q1964=makeQuery(id+"F13.opPattern","COPY",BODY,{"derivedFrom":makeQuery(id+"F11.opPattern","COPY",BODY,{"derivedFrom":makeQuery(id+"F7.opPattern","COPY",BODY,{"derivedFrom":makeQuery(id+"F6.opPattern","COPY",BODY,{"derivedFrom":makeQuery(id+"F5.opPattern","COPY",BODY,{"derivedFrom":makeQuery(id+"F4.opPattern","COPY",BODY,{"derivedFrom":makeQuery(id+"F1.opRevolve","SWEPT_BODY",BODY,{"disambiguationData":[OSD([sQuery(id+"F0.wireOp",EDGE,"E1")])]}),"instanceName":"1"}),"instanceName":"1"}),"instanceName":"1"}),"instanceName":"1"}),"instanceName":"1"}),"instanceName":"1"});
            var Q1965;
            Q1965=makeQuery(id+"F13.opPattern","COPY",BODY,{"derivedFrom":makeQuery(id+"F11.opPattern","COPY",BODY,{"derivedFrom":makeQuery(id+"F7.opPattern","COPY",BODY,{"derivedFrom":makeQuery(id+"F6.opPattern","COPY",BODY,{"derivedFrom":makeQuery(id+"F5.opPattern","COPY",BODY,{"derivedFrom":makeQuery(id+"F4.opPattern","COPY",BODY,{"derivedFrom":makeQuery(id+"F2.opPattern","COPY",BODY,{"derivedFrom":makeQuery(id+"F1.opRevolve","SWEPT_BODY",BODY,{"disambiguationData":[OSD([sQuery(id+"F0.wireOp",EDGE,"E1")])]}),"instanceName":"1"}),"instanceName":"1"}),"instanceName":"1"}),"instanceName":"1"}),"instanceName":"1"}),"instanceName":"1"}),"instanceName":"1"});
            var Q1966;
            Q1966=makeQuery(id+"F13.opPattern","COPY",BODY,{"derivedFrom":makeQuery(id+"F11.opPattern","COPY",BODY,{"derivedFrom":makeQuery(id+"F7.opPattern","COPY",BODY,{"derivedFrom":makeQuery(id+"F6.opPattern","COPY",BODY,{"derivedFrom":makeQuery(id+"F5.opPattern","COPY",BODY,{"derivedFrom":makeQuery(id+"F4.opPattern","COPY",BODY,{"derivedFrom":makeQuery(id+"F3.opPattern","COPY",BODY,{"derivedFrom":makeQuery(id+"F2.opPattern","COPY",BODY,{"derivedFrom":makeQuery(id+"F1.opRevolve","SWEPT_BODY",BODY,{"disambiguationData":[OSD([sQuery(id+"F0.wireOp",EDGE,"E1")])]}),"instanceName":"1"}),"instanceName":"1"}),"instanceName":"1"}),"instanceName":"1"}),"instanceName":"1"}),"instanceName":"1"}),"instanceName":"1"}),"instanceName":"1"});
            var Q1967;
            Q1967=makeQuery(id+"F13.opPattern","COPY",BODY,{"derivedFrom":makeQuery(id+"F11.opPattern","COPY",BODY,{"derivedFrom":makeQuery(id+"F8.opPattern","COPY",BODY,{"derivedFrom":makeQuery(id+"F1.opRevolve","SWEPT_BODY",BODY,{"disambiguationData":[OSD([sQuery(id+"F0.wireOp",EDGE,"E1")])]}),"instanceName":"1"}),"instanceName":"1"}),"instanceName":"1"});
            var Q1968;
            Q1968=makeQuery(id+"F13.opPattern","COPY",BODY,{"derivedFrom":makeQuery(id+"F11.opPattern","COPY",BODY,{"derivedFrom":makeQuery(id+"F8.opPattern","COPY",BODY,{"derivedFrom":makeQuery(id+"F2.opPattern","COPY",BODY,{"derivedFrom":makeQuery(id+"F1.opRevolve","SWEPT_BODY",BODY,{"disambiguationData":[OSD([sQuery(id+"F0.wireOp",EDGE,"E1")])]}),"instanceName":"1"}),"instanceName":"1"}),"instanceName":"1"}),"instanceName":"1"});
            var Q1969;
            Q1969=makeQuery(id+"F13.opPattern","COPY",BODY,{"derivedFrom":makeQuery(id+"F11.opPattern","COPY",BODY,{"derivedFrom":makeQuery(id+"F8.opPattern","COPY",BODY,{"derivedFrom":makeQuery(id+"F3.opPattern","COPY",BODY,{"derivedFrom":makeQuery(id+"F2.opPattern","COPY",BODY,{"derivedFrom":makeQuery(id+"F1.opRevolve","SWEPT_BODY",BODY,{"disambiguationData":[OSD([sQuery(id+"F0.wireOp",EDGE,"E1")])]}),"instanceName":"1"}),"instanceName":"1"}),"instanceName":"1"}),"instanceName":"1"}),"instanceName":"1"});
            var Q1970;
            Q1970=makeQuery(id+"F13.opPattern","COPY",BODY,{"derivedFrom":makeQuery(id+"F11.opPattern","COPY",BODY,{"derivedFrom":makeQuery(id+"F8.opPattern","COPY",BODY,{"derivedFrom":makeQuery(id+"F4.opPattern","COPY",BODY,{"derivedFrom":makeQuery(id+"F1.opRevolve","SWEPT_BODY",BODY,{"disambiguationData":[OSD([sQuery(id+"F0.wireOp",EDGE,"E1")])]}),"instanceName":"1"}),"instanceName":"1"}),"instanceName":"1"}),"instanceName":"1"});
            var Q1971;
            Q1971=makeQuery(id+"F13.opPattern","COPY",BODY,{"derivedFrom":makeQuery(id+"F11.opPattern","COPY",BODY,{"derivedFrom":makeQuery(id+"F8.opPattern","COPY",BODY,{"derivedFrom":makeQuery(id+"F4.opPattern","COPY",BODY,{"derivedFrom":makeQuery(id+"F2.opPattern","COPY",BODY,{"derivedFrom":makeQuery(id+"F1.opRevolve","SWEPT_BODY",BODY,{"disambiguationData":[OSD([sQuery(id+"F0.wireOp",EDGE,"E1")])]}),"instanceName":"1"}),"instanceName":"1"}),"instanceName":"1"}),"instanceName":"1"}),"instanceName":"1"});
            var Q1972;
            Q1972=makeQuery(id+"F13.opPattern","COPY",BODY,{"derivedFrom":makeQuery(id+"F11.opPattern","COPY",BODY,{"derivedFrom":makeQuery(id+"F8.opPattern","COPY",BODY,{"derivedFrom":makeQuery(id+"F4.opPattern","COPY",BODY,{"derivedFrom":makeQuery(id+"F3.opPattern","COPY",BODY,{"derivedFrom":makeQuery(id+"F2.opPattern","COPY",BODY,{"derivedFrom":makeQuery(id+"F1.opRevolve","SWEPT_BODY",BODY,{"disambiguationData":[OSD([sQuery(id+"F0.wireOp",EDGE,"E1")])]}),"instanceName":"1"}),"instanceName":"1"}),"instanceName":"1"}),"instanceName":"1"}),"instanceName":"1"}),"instanceName":"1"});
            var Q1973;
            Q1973=makeQuery(id+"F13.opPattern","COPY",BODY,{"derivedFrom":makeQuery(id+"F11.opPattern","COPY",BODY,{"derivedFrom":makeQuery(id+"F8.opPattern","COPY",BODY,{"derivedFrom":makeQuery(id+"F5.opPattern","COPY",BODY,{"derivedFrom":makeQuery(id+"F1.opRevolve","SWEPT_BODY",BODY,{"disambiguationData":[OSD([sQuery(id+"F0.wireOp",EDGE,"E1")])]}),"instanceName":"1"}),"instanceName":"1"}),"instanceName":"1"}),"instanceName":"1"});
            var Q1974;
            Q1974=makeQuery(id+"F13.opPattern","COPY",BODY,{"derivedFrom":makeQuery(id+"F11.opPattern","COPY",BODY,{"derivedFrom":makeQuery(id+"F8.opPattern","COPY",BODY,{"derivedFrom":makeQuery(id+"F5.opPattern","COPY",BODY,{"derivedFrom":makeQuery(id+"F2.opPattern","COPY",BODY,{"derivedFrom":makeQuery(id+"F1.opRevolve","SWEPT_BODY",BODY,{"disambiguationData":[OSD([sQuery(id+"F0.wireOp",EDGE,"E1")])]}),"instanceName":"1"}),"instanceName":"1"}),"instanceName":"1"}),"instanceName":"1"}),"instanceName":"1"});
            var Q1975;
            Q1975=makeQuery(id+"F13.opPattern","COPY",BODY,{"derivedFrom":makeQuery(id+"F11.opPattern","COPY",BODY,{"derivedFrom":makeQuery(id+"F8.opPattern","COPY",BODY,{"derivedFrom":makeQuery(id+"F5.opPattern","COPY",BODY,{"derivedFrom":makeQuery(id+"F3.opPattern","COPY",BODY,{"derivedFrom":makeQuery(id+"F2.opPattern","COPY",BODY,{"derivedFrom":makeQuery(id+"F1.opRevolve","SWEPT_BODY",BODY,{"disambiguationData":[OSD([sQuery(id+"F0.wireOp",EDGE,"E1")])]}),"instanceName":"1"}),"instanceName":"1"}),"instanceName":"1"}),"instanceName":"1"}),"instanceName":"1"}),"instanceName":"1"});
            var Q1976;
            Q1976=makeQuery(id+"F13.opPattern","COPY",BODY,{"derivedFrom":makeQuery(id+"F11.opPattern","COPY",BODY,{"derivedFrom":makeQuery(id+"F8.opPattern","COPY",BODY,{"derivedFrom":makeQuery(id+"F5.opPattern","COPY",BODY,{"derivedFrom":makeQuery(id+"F4.opPattern","COPY",BODY,{"derivedFrom":makeQuery(id+"F1.opRevolve","SWEPT_BODY",BODY,{"disambiguationData":[OSD([sQuery(id+"F0.wireOp",EDGE,"E1")])]}),"instanceName":"1"}),"instanceName":"1"}),"instanceName":"1"}),"instanceName":"1"}),"instanceName":"1"});
            var Q1977;
            Q1977=makeQuery(id+"F13.opPattern","COPY",BODY,{"derivedFrom":makeQuery(id+"F11.opPattern","COPY",BODY,{"derivedFrom":makeQuery(id+"F8.opPattern","COPY",BODY,{"derivedFrom":makeQuery(id+"F5.opPattern","COPY",BODY,{"derivedFrom":makeQuery(id+"F4.opPattern","COPY",BODY,{"derivedFrom":makeQuery(id+"F2.opPattern","COPY",BODY,{"derivedFrom":makeQuery(id+"F1.opRevolve","SWEPT_BODY",BODY,{"disambiguationData":[OSD([sQuery(id+"F0.wireOp",EDGE,"E1")])]}),"instanceName":"1"}),"instanceName":"1"}),"instanceName":"1"}),"instanceName":"1"}),"instanceName":"1"}),"instanceName":"1"});
            var Q1978;
            Q1978=makeQuery(id+"F13.opPattern","COPY",BODY,{"derivedFrom":makeQuery(id+"F11.opPattern","COPY",BODY,{"derivedFrom":makeQuery(id+"F8.opPattern","COPY",BODY,{"derivedFrom":makeQuery(id+"F5.opPattern","COPY",BODY,{"derivedFrom":makeQuery(id+"F4.opPattern","COPY",BODY,{"derivedFrom":makeQuery(id+"F3.opPattern","COPY",BODY,{"derivedFrom":makeQuery(id+"F2.opPattern","COPY",BODY,{"derivedFrom":makeQuery(id+"F1.opRevolve","SWEPT_BODY",BODY,{"disambiguationData":[OSD([sQuery(id+"F0.wireOp",EDGE,"E1")])]}),"instanceName":"1"}),"instanceName":"1"}),"instanceName":"1"}),"instanceName":"1"}),"instanceName":"1"}),"instanceName":"1"}),"instanceName":"1"});
            var Q1979;
            Q1979=makeQuery(id+"F13.opPattern","COPY",BODY,{"derivedFrom":makeQuery(id+"F11.opPattern","COPY",BODY,{"derivedFrom":makeQuery(id+"F8.opPattern","COPY",BODY,{"derivedFrom":makeQuery(id+"F6.opPattern","COPY",BODY,{"derivedFrom":makeQuery(id+"F1.opRevolve","SWEPT_BODY",BODY,{"disambiguationData":[OSD([sQuery(id+"F0.wireOp",EDGE,"E1")])]}),"instanceName":"1"}),"instanceName":"1"}),"instanceName":"1"}),"instanceName":"1"});
            var Q1980;
            Q1980=makeQuery(id+"F13.opPattern","COPY",BODY,{"derivedFrom":makeQuery(id+"F11.opPattern","COPY",BODY,{"derivedFrom":makeQuery(id+"F8.opPattern","COPY",BODY,{"derivedFrom":makeQuery(id+"F6.opPattern","COPY",BODY,{"derivedFrom":makeQuery(id+"F2.opPattern","COPY",BODY,{"derivedFrom":makeQuery(id+"F1.opRevolve","SWEPT_BODY",BODY,{"disambiguationData":[OSD([sQuery(id+"F0.wireOp",EDGE,"E1")])]}),"instanceName":"1"}),"instanceName":"1"}),"instanceName":"1"}),"instanceName":"1"}),"instanceName":"1"});
            var Q1981;
            Q1981=makeQuery(id+"F13.opPattern","COPY",BODY,{"derivedFrom":makeQuery(id+"F11.opPattern","COPY",BODY,{"derivedFrom":makeQuery(id+"F8.opPattern","COPY",BODY,{"derivedFrom":makeQuery(id+"F6.opPattern","COPY",BODY,{"derivedFrom":makeQuery(id+"F3.opPattern","COPY",BODY,{"derivedFrom":makeQuery(id+"F2.opPattern","COPY",BODY,{"derivedFrom":makeQuery(id+"F1.opRevolve","SWEPT_BODY",BODY,{"disambiguationData":[OSD([sQuery(id+"F0.wireOp",EDGE,"E1")])]}),"instanceName":"1"}),"instanceName":"1"}),"instanceName":"1"}),"instanceName":"1"}),"instanceName":"1"}),"instanceName":"1"});
            var Q1982;
            Q1982=makeQuery(id+"F13.opPattern","COPY",BODY,{"derivedFrom":makeQuery(id+"F11.opPattern","COPY",BODY,{"derivedFrom":makeQuery(id+"F8.opPattern","COPY",BODY,{"derivedFrom":makeQuery(id+"F6.opPattern","COPY",BODY,{"derivedFrom":makeQuery(id+"F4.opPattern","COPY",BODY,{"derivedFrom":makeQuery(id+"F1.opRevolve","SWEPT_BODY",BODY,{"disambiguationData":[OSD([sQuery(id+"F0.wireOp",EDGE,"E1")])]}),"instanceName":"1"}),"instanceName":"1"}),"instanceName":"1"}),"instanceName":"1"}),"instanceName":"1"});
            var Q1983;
            Q1983=makeQuery(id+"F13.opPattern","COPY",BODY,{"derivedFrom":makeQuery(id+"F11.opPattern","COPY",BODY,{"derivedFrom":makeQuery(id+"F8.opPattern","COPY",BODY,{"derivedFrom":makeQuery(id+"F6.opPattern","COPY",BODY,{"derivedFrom":makeQuery(id+"F4.opPattern","COPY",BODY,{"derivedFrom":makeQuery(id+"F2.opPattern","COPY",BODY,{"derivedFrom":makeQuery(id+"F1.opRevolve","SWEPT_BODY",BODY,{"disambiguationData":[OSD([sQuery(id+"F0.wireOp",EDGE,"E1")])]}),"instanceName":"1"}),"instanceName":"1"}),"instanceName":"1"}),"instanceName":"1"}),"instanceName":"1"}),"instanceName":"1"});
            var Q1984;
            Q1984=makeQuery(id+"F13.opPattern","COPY",BODY,{"derivedFrom":makeQuery(id+"F11.opPattern","COPY",BODY,{"derivedFrom":makeQuery(id+"F8.opPattern","COPY",BODY,{"derivedFrom":makeQuery(id+"F6.opPattern","COPY",BODY,{"derivedFrom":makeQuery(id+"F4.opPattern","COPY",BODY,{"derivedFrom":makeQuery(id+"F3.opPattern","COPY",BODY,{"derivedFrom":makeQuery(id+"F2.opPattern","COPY",BODY,{"derivedFrom":makeQuery(id+"F1.opRevolve","SWEPT_BODY",BODY,{"disambiguationData":[OSD([sQuery(id+"F0.wireOp",EDGE,"E1")])]}),"instanceName":"1"}),"instanceName":"1"}),"instanceName":"1"}),"instanceName":"1"}),"instanceName":"1"}),"instanceName":"1"}),"instanceName":"1"});
            var Q1985;
            Q1985=makeQuery(id+"F13.opPattern","COPY",BODY,{"derivedFrom":makeQuery(id+"F11.opPattern","COPY",BODY,{"derivedFrom":makeQuery(id+"F8.opPattern","COPY",BODY,{"derivedFrom":makeQuery(id+"F6.opPattern","COPY",BODY,{"derivedFrom":makeQuery(id+"F5.opPattern","COPY",BODY,{"derivedFrom":makeQuery(id+"F1.opRevolve","SWEPT_BODY",BODY,{"disambiguationData":[OSD([sQuery(id+"F0.wireOp",EDGE,"E1")])]}),"instanceName":"1"}),"instanceName":"1"}),"instanceName":"1"}),"instanceName":"1"}),"instanceName":"1"});
            var Q1986;
            Q1986=makeQuery(id+"F13.opPattern","COPY",BODY,{"derivedFrom":makeQuery(id+"F11.opPattern","COPY",BODY,{"derivedFrom":makeQuery(id+"F8.opPattern","COPY",BODY,{"derivedFrom":makeQuery(id+"F6.opPattern","COPY",BODY,{"derivedFrom":makeQuery(id+"F5.opPattern","COPY",BODY,{"derivedFrom":makeQuery(id+"F2.opPattern","COPY",BODY,{"derivedFrom":makeQuery(id+"F1.opRevolve","SWEPT_BODY",BODY,{"disambiguationData":[OSD([sQuery(id+"F0.wireOp",EDGE,"E1")])]}),"instanceName":"1"}),"instanceName":"1"}),"instanceName":"1"}),"instanceName":"1"}),"instanceName":"1"}),"instanceName":"1"});
            var Q1987;
            Q1987=makeQuery(id+"F13.opPattern","COPY",BODY,{"derivedFrom":makeQuery(id+"F11.opPattern","COPY",BODY,{"derivedFrom":makeQuery(id+"F8.opPattern","COPY",BODY,{"derivedFrom":makeQuery(id+"F6.opPattern","COPY",BODY,{"derivedFrom":makeQuery(id+"F5.opPattern","COPY",BODY,{"derivedFrom":makeQuery(id+"F3.opPattern","COPY",BODY,{"derivedFrom":makeQuery(id+"F2.opPattern","COPY",BODY,{"derivedFrom":makeQuery(id+"F1.opRevolve","SWEPT_BODY",BODY,{"disambiguationData":[OSD([sQuery(id+"F0.wireOp",EDGE,"E1")])]}),"instanceName":"1"}),"instanceName":"1"}),"instanceName":"1"}),"instanceName":"1"}),"instanceName":"1"}),"instanceName":"1"}),"instanceName":"1"});
            var Q1988;
            Q1988=makeQuery(id+"F13.opPattern","COPY",BODY,{"derivedFrom":makeQuery(id+"F11.opPattern","COPY",BODY,{"derivedFrom":makeQuery(id+"F8.opPattern","COPY",BODY,{"derivedFrom":makeQuery(id+"F6.opPattern","COPY",BODY,{"derivedFrom":makeQuery(id+"F5.opPattern","COPY",BODY,{"derivedFrom":makeQuery(id+"F4.opPattern","COPY",BODY,{"derivedFrom":makeQuery(id+"F1.opRevolve","SWEPT_BODY",BODY,{"disambiguationData":[OSD([sQuery(id+"F0.wireOp",EDGE,"E1")])]}),"instanceName":"1"}),"instanceName":"1"}),"instanceName":"1"}),"instanceName":"1"}),"instanceName":"1"}),"instanceName":"1"});
            var Q1989;
            Q1989=makeQuery(id+"F13.opPattern","COPY",BODY,{"derivedFrom":makeQuery(id+"F11.opPattern","COPY",BODY,{"derivedFrom":makeQuery(id+"F8.opPattern","COPY",BODY,{"derivedFrom":makeQuery(id+"F6.opPattern","COPY",BODY,{"derivedFrom":makeQuery(id+"F5.opPattern","COPY",BODY,{"derivedFrom":makeQuery(id+"F4.opPattern","COPY",BODY,{"derivedFrom":makeQuery(id+"F2.opPattern","COPY",BODY,{"derivedFrom":makeQuery(id+"F1.opRevolve","SWEPT_BODY",BODY,{"disambiguationData":[OSD([sQuery(id+"F0.wireOp",EDGE,"E1")])]}),"instanceName":"1"}),"instanceName":"1"}),"instanceName":"1"}),"instanceName":"1"}),"instanceName":"1"}),"instanceName":"1"}),"instanceName":"1"});
            var Q1990;
            Q1990=makeQuery(id+"F13.opPattern","COPY",BODY,{"derivedFrom":makeQuery(id+"F11.opPattern","COPY",BODY,{"derivedFrom":makeQuery(id+"F8.opPattern","COPY",BODY,{"derivedFrom":makeQuery(id+"F6.opPattern","COPY",BODY,{"derivedFrom":makeQuery(id+"F5.opPattern","COPY",BODY,{"derivedFrom":makeQuery(id+"F4.opPattern","COPY",BODY,{"derivedFrom":makeQuery(id+"F3.opPattern","COPY",BODY,{"derivedFrom":makeQuery(id+"F2.opPattern","COPY",BODY,{"derivedFrom":makeQuery(id+"F1.opRevolve","SWEPT_BODY",BODY,{"disambiguationData":[OSD([sQuery(id+"F0.wireOp",EDGE,"E1")])]}),"instanceName":"1"}),"instanceName":"1"}),"instanceName":"1"}),"instanceName":"1"}),"instanceName":"1"}),"instanceName":"1"}),"instanceName":"1"}),"instanceName":"1"});
            var Q1991;
            Q1991=makeQuery(id+"F13.opPattern","COPY",BODY,{"derivedFrom":makeQuery(id+"F11.opPattern","COPY",BODY,{"derivedFrom":makeQuery(id+"F8.opPattern","COPY",BODY,{"derivedFrom":makeQuery(id+"F7.opPattern","COPY",BODY,{"derivedFrom":makeQuery(id+"F1.opRevolve","SWEPT_BODY",BODY,{"disambiguationData":[OSD([sQuery(id+"F0.wireOp",EDGE,"E1")])]}),"instanceName":"1"}),"instanceName":"1"}),"instanceName":"1"}),"instanceName":"1"});
            var Q1992;
            Q1992=makeQuery(id+"F13.opPattern","COPY",BODY,{"derivedFrom":makeQuery(id+"F11.opPattern","COPY",BODY,{"derivedFrom":makeQuery(id+"F8.opPattern","COPY",BODY,{"derivedFrom":makeQuery(id+"F7.opPattern","COPY",BODY,{"derivedFrom":makeQuery(id+"F2.opPattern","COPY",BODY,{"derivedFrom":makeQuery(id+"F1.opRevolve","SWEPT_BODY",BODY,{"disambiguationData":[OSD([sQuery(id+"F0.wireOp",EDGE,"E1")])]}),"instanceName":"1"}),"instanceName":"1"}),"instanceName":"1"}),"instanceName":"1"}),"instanceName":"1"});
            var Q1993;
            Q1993=makeQuery(id+"F13.opPattern","COPY",BODY,{"derivedFrom":makeQuery(id+"F11.opPattern","COPY",BODY,{"derivedFrom":makeQuery(id+"F8.opPattern","COPY",BODY,{"derivedFrom":makeQuery(id+"F7.opPattern","COPY",BODY,{"derivedFrom":makeQuery(id+"F3.opPattern","COPY",BODY,{"derivedFrom":makeQuery(id+"F2.opPattern","COPY",BODY,{"derivedFrom":makeQuery(id+"F1.opRevolve","SWEPT_BODY",BODY,{"disambiguationData":[OSD([sQuery(id+"F0.wireOp",EDGE,"E1")])]}),"instanceName":"1"}),"instanceName":"1"}),"instanceName":"1"}),"instanceName":"1"}),"instanceName":"1"}),"instanceName":"1"});
            var Q1994;
            Q1994=makeQuery(id+"F13.opPattern","COPY",BODY,{"derivedFrom":makeQuery(id+"F11.opPattern","COPY",BODY,{"derivedFrom":makeQuery(id+"F8.opPattern","COPY",BODY,{"derivedFrom":makeQuery(id+"F7.opPattern","COPY",BODY,{"derivedFrom":makeQuery(id+"F4.opPattern","COPY",BODY,{"derivedFrom":makeQuery(id+"F1.opRevolve","SWEPT_BODY",BODY,{"disambiguationData":[OSD([sQuery(id+"F0.wireOp",EDGE,"E1")])]}),"instanceName":"1"}),"instanceName":"1"}),"instanceName":"1"}),"instanceName":"1"}),"instanceName":"1"});
            var Q1995;
            Q1995=makeQuery(id+"F13.opPattern","COPY",BODY,{"derivedFrom":makeQuery(id+"F11.opPattern","COPY",BODY,{"derivedFrom":makeQuery(id+"F8.opPattern","COPY",BODY,{"derivedFrom":makeQuery(id+"F7.opPattern","COPY",BODY,{"derivedFrom":makeQuery(id+"F4.opPattern","COPY",BODY,{"derivedFrom":makeQuery(id+"F2.opPattern","COPY",BODY,{"derivedFrom":makeQuery(id+"F1.opRevolve","SWEPT_BODY",BODY,{"disambiguationData":[OSD([sQuery(id+"F0.wireOp",EDGE,"E1")])]}),"instanceName":"1"}),"instanceName":"1"}),"instanceName":"1"}),"instanceName":"1"}),"instanceName":"1"}),"instanceName":"1"});
            var Q1996;
            Q1996=makeQuery(id+"F13.opPattern","COPY",BODY,{"derivedFrom":makeQuery(id+"F11.opPattern","COPY",BODY,{"derivedFrom":makeQuery(id+"F8.opPattern","COPY",BODY,{"derivedFrom":makeQuery(id+"F7.opPattern","COPY",BODY,{"derivedFrom":makeQuery(id+"F4.opPattern","COPY",BODY,{"derivedFrom":makeQuery(id+"F3.opPattern","COPY",BODY,{"derivedFrom":makeQuery(id+"F2.opPattern","COPY",BODY,{"derivedFrom":makeQuery(id+"F1.opRevolve","SWEPT_BODY",BODY,{"disambiguationData":[OSD([sQuery(id+"F0.wireOp",EDGE,"E1")])]}),"instanceName":"1"}),"instanceName":"1"}),"instanceName":"1"}),"instanceName":"1"}),"instanceName":"1"}),"instanceName":"1"}),"instanceName":"1"});
            var Q1997;
            Q1997=makeQuery(id+"F13.opPattern","COPY",BODY,{"derivedFrom":makeQuery(id+"F11.opPattern","COPY",BODY,{"derivedFrom":makeQuery(id+"F8.opPattern","COPY",BODY,{"derivedFrom":makeQuery(id+"F7.opPattern","COPY",BODY,{"derivedFrom":makeQuery(id+"F5.opPattern","COPY",BODY,{"derivedFrom":makeQuery(id+"F1.opRevolve","SWEPT_BODY",BODY,{"disambiguationData":[OSD([sQuery(id+"F0.wireOp",EDGE,"E1")])]}),"instanceName":"1"}),"instanceName":"1"}),"instanceName":"1"}),"instanceName":"1"}),"instanceName":"1"});
            var Q1998;
            Q1998=makeQuery(id+"F13.opPattern","COPY",BODY,{"derivedFrom":makeQuery(id+"F11.opPattern","COPY",BODY,{"derivedFrom":makeQuery(id+"F8.opPattern","COPY",BODY,{"derivedFrom":makeQuery(id+"F7.opPattern","COPY",BODY,{"derivedFrom":makeQuery(id+"F5.opPattern","COPY",BODY,{"derivedFrom":makeQuery(id+"F2.opPattern","COPY",BODY,{"derivedFrom":makeQuery(id+"F1.opRevolve","SWEPT_BODY",BODY,{"disambiguationData":[OSD([sQuery(id+"F0.wireOp",EDGE,"E1")])]}),"instanceName":"1"}),"instanceName":"1"}),"instanceName":"1"}),"instanceName":"1"}),"instanceName":"1"}),"instanceName":"1"});
            var Q1999;
            Q1999=makeQuery(id+"F13.opPattern","COPY",BODY,{"derivedFrom":makeQuery(id+"F11.opPattern","COPY",BODY,{"derivedFrom":makeQuery(id+"F8.opPattern","COPY",BODY,{"derivedFrom":makeQuery(id+"F7.opPattern","COPY",BODY,{"derivedFrom":makeQuery(id+"F5.opPattern","COPY",BODY,{"derivedFrom":makeQuery(id+"F3.opPattern","COPY",BODY,{"derivedFrom":makeQuery(id+"F2.opPattern","COPY",BODY,{"derivedFrom":makeQuery(id+"F1.opRevolve","SWEPT_BODY",BODY,{"disambiguationData":[OSD([sQuery(id+"F0.wireOp",EDGE,"E1")])]}),"instanceName":"1"}),"instanceName":"1"}),"instanceName":"1"}),"instanceName":"1"}),"instanceName":"1"}),"instanceName":"1"}),"instanceName":"1"});
            var Q2000;
            Q2000=makeQuery(id+"F13.opPattern","COPY",BODY,{"derivedFrom":makeQuery(id+"F11.opPattern","COPY",BODY,{"derivedFrom":makeQuery(id+"F8.opPattern","COPY",BODY,{"derivedFrom":makeQuery(id+"F7.opPattern","COPY",BODY,{"derivedFrom":makeQuery(id+"F5.opPattern","COPY",BODY,{"derivedFrom":makeQuery(id+"F4.opPattern","COPY",BODY,{"derivedFrom":makeQuery(id+"F1.opRevolve","SWEPT_BODY",BODY,{"disambiguationData":[OSD([sQuery(id+"F0.wireOp",EDGE,"E1")])]}),"instanceName":"1"}),"instanceName":"1"}),"instanceName":"1"}),"instanceName":"1"}),"instanceName":"1"}),"instanceName":"1"});
            var Q2001;
            Q2001=makeQuery(id+"F13.opPattern","COPY",BODY,{"derivedFrom":makeQuery(id+"F11.opPattern","COPY",BODY,{"derivedFrom":makeQuery(id+"F8.opPattern","COPY",BODY,{"derivedFrom":makeQuery(id+"F7.opPattern","COPY",BODY,{"derivedFrom":makeQuery(id+"F5.opPattern","COPY",BODY,{"derivedFrom":makeQuery(id+"F4.opPattern","COPY",BODY,{"derivedFrom":makeQuery(id+"F2.opPattern","COPY",BODY,{"derivedFrom":makeQuery(id+"F1.opRevolve","SWEPT_BODY",BODY,{"disambiguationData":[OSD([sQuery(id+"F0.wireOp",EDGE,"E1")])]}),"instanceName":"1"}),"instanceName":"1"}),"instanceName":"1"}),"instanceName":"1"}),"instanceName":"1"}),"instanceName":"1"}),"instanceName":"1"});
            var Q2002;
            Q2002=makeQuery(id+"F13.opPattern","COPY",BODY,{"derivedFrom":makeQuery(id+"F11.opPattern","COPY",BODY,{"derivedFrom":makeQuery(id+"F8.opPattern","COPY",BODY,{"derivedFrom":makeQuery(id+"F7.opPattern","COPY",BODY,{"derivedFrom":makeQuery(id+"F5.opPattern","COPY",BODY,{"derivedFrom":makeQuery(id+"F4.opPattern","COPY",BODY,{"derivedFrom":makeQuery(id+"F3.opPattern","COPY",BODY,{"derivedFrom":makeQuery(id+"F2.opPattern","COPY",BODY,{"derivedFrom":makeQuery(id+"F1.opRevolve","SWEPT_BODY",BODY,{"disambiguationData":[OSD([sQuery(id+"F0.wireOp",EDGE,"E1")])]}),"instanceName":"1"}),"instanceName":"1"}),"instanceName":"1"}),"instanceName":"1"}),"instanceName":"1"}),"instanceName":"1"}),"instanceName":"1"}),"instanceName":"1"});
            var Q2003;
            Q2003=makeQuery(id+"F13.opPattern","COPY",BODY,{"derivedFrom":makeQuery(id+"F11.opPattern","COPY",BODY,{"derivedFrom":makeQuery(id+"F8.opPattern","COPY",BODY,{"derivedFrom":makeQuery(id+"F7.opPattern","COPY",BODY,{"derivedFrom":makeQuery(id+"F6.opPattern","COPY",BODY,{"derivedFrom":makeQuery(id+"F1.opRevolve","SWEPT_BODY",BODY,{"disambiguationData":[OSD([sQuery(id+"F0.wireOp",EDGE,"E1")])]}),"instanceName":"1"}),"instanceName":"1"}),"instanceName":"1"}),"instanceName":"1"}),"instanceName":"1"});
            var Q2004;
            Q2004=makeQuery(id+"F13.opPattern","COPY",BODY,{"derivedFrom":makeQuery(id+"F11.opPattern","COPY",BODY,{"derivedFrom":makeQuery(id+"F8.opPattern","COPY",BODY,{"derivedFrom":makeQuery(id+"F7.opPattern","COPY",BODY,{"derivedFrom":makeQuery(id+"F6.opPattern","COPY",BODY,{"derivedFrom":makeQuery(id+"F2.opPattern","COPY",BODY,{"derivedFrom":makeQuery(id+"F1.opRevolve","SWEPT_BODY",BODY,{"disambiguationData":[OSD([sQuery(id+"F0.wireOp",EDGE,"E1")])]}),"instanceName":"1"}),"instanceName":"1"}),"instanceName":"1"}),"instanceName":"1"}),"instanceName":"1"}),"instanceName":"1"});
            var Q2005;
            Q2005=makeQuery(id+"F13.opPattern","COPY",BODY,{"derivedFrom":makeQuery(id+"F11.opPattern","COPY",BODY,{"derivedFrom":makeQuery(id+"F8.opPattern","COPY",BODY,{"derivedFrom":makeQuery(id+"F7.opPattern","COPY",BODY,{"derivedFrom":makeQuery(id+"F6.opPattern","COPY",BODY,{"derivedFrom":makeQuery(id+"F3.opPattern","COPY",BODY,{"derivedFrom":makeQuery(id+"F2.opPattern","COPY",BODY,{"derivedFrom":makeQuery(id+"F1.opRevolve","SWEPT_BODY",BODY,{"disambiguationData":[OSD([sQuery(id+"F0.wireOp",EDGE,"E1")])]}),"instanceName":"1"}),"instanceName":"1"}),"instanceName":"1"}),"instanceName":"1"}),"instanceName":"1"}),"instanceName":"1"}),"instanceName":"1"});
            var Q2006;
            Q2006=makeQuery(id+"F13.opPattern","COPY",BODY,{"derivedFrom":makeQuery(id+"F11.opPattern","COPY",BODY,{"derivedFrom":makeQuery(id+"F8.opPattern","COPY",BODY,{"derivedFrom":makeQuery(id+"F7.opPattern","COPY",BODY,{"derivedFrom":makeQuery(id+"F6.opPattern","COPY",BODY,{"derivedFrom":makeQuery(id+"F4.opPattern","COPY",BODY,{"derivedFrom":makeQuery(id+"F1.opRevolve","SWEPT_BODY",BODY,{"disambiguationData":[OSD([sQuery(id+"F0.wireOp",EDGE,"E1")])]}),"instanceName":"1"}),"instanceName":"1"}),"instanceName":"1"}),"instanceName":"1"}),"instanceName":"1"}),"instanceName":"1"});
            var Q2007;
            Q2007=makeQuery(id+"F13.opPattern","COPY",BODY,{"derivedFrom":makeQuery(id+"F11.opPattern","COPY",BODY,{"derivedFrom":makeQuery(id+"F8.opPattern","COPY",BODY,{"derivedFrom":makeQuery(id+"F7.opPattern","COPY",BODY,{"derivedFrom":makeQuery(id+"F6.opPattern","COPY",BODY,{"derivedFrom":makeQuery(id+"F4.opPattern","COPY",BODY,{"derivedFrom":makeQuery(id+"F2.opPattern","COPY",BODY,{"derivedFrom":makeQuery(id+"F1.opRevolve","SWEPT_BODY",BODY,{"disambiguationData":[OSD([sQuery(id+"F0.wireOp",EDGE,"E1")])]}),"instanceName":"1"}),"instanceName":"1"}),"instanceName":"1"}),"instanceName":"1"}),"instanceName":"1"}),"instanceName":"1"}),"instanceName":"1"});
            var Q2008;
            Q2008=makeQuery(id+"F13.opPattern","COPY",BODY,{"derivedFrom":makeQuery(id+"F11.opPattern","COPY",BODY,{"derivedFrom":makeQuery(id+"F8.opPattern","COPY",BODY,{"derivedFrom":makeQuery(id+"F7.opPattern","COPY",BODY,{"derivedFrom":makeQuery(id+"F6.opPattern","COPY",BODY,{"derivedFrom":makeQuery(id+"F4.opPattern","COPY",BODY,{"derivedFrom":makeQuery(id+"F3.opPattern","COPY",BODY,{"derivedFrom":makeQuery(id+"F2.opPattern","COPY",BODY,{"derivedFrom":makeQuery(id+"F1.opRevolve","SWEPT_BODY",BODY,{"disambiguationData":[OSD([sQuery(id+"F0.wireOp",EDGE,"E1")])]}),"instanceName":"1"}),"instanceName":"1"}),"instanceName":"1"}),"instanceName":"1"}),"instanceName":"1"}),"instanceName":"1"}),"instanceName":"1"}),"instanceName":"1"});
            var Q2009;
            Q2009=makeQuery(id+"F13.opPattern","COPY",BODY,{"derivedFrom":makeQuery(id+"F11.opPattern","COPY",BODY,{"derivedFrom":makeQuery(id+"F8.opPattern","COPY",BODY,{"derivedFrom":makeQuery(id+"F7.opPattern","COPY",BODY,{"derivedFrom":makeQuery(id+"F6.opPattern","COPY",BODY,{"derivedFrom":makeQuery(id+"F5.opPattern","COPY",BODY,{"derivedFrom":makeQuery(id+"F1.opRevolve","SWEPT_BODY",BODY,{"disambiguationData":[OSD([sQuery(id+"F0.wireOp",EDGE,"E1")])]}),"instanceName":"1"}),"instanceName":"1"}),"instanceName":"1"}),"instanceName":"1"}),"instanceName":"1"}),"instanceName":"1"});
            var Q2010;
            Q2010=makeQuery(id+"F13.opPattern","COPY",BODY,{"derivedFrom":makeQuery(id+"F11.opPattern","COPY",BODY,{"derivedFrom":makeQuery(id+"F8.opPattern","COPY",BODY,{"derivedFrom":makeQuery(id+"F7.opPattern","COPY",BODY,{"derivedFrom":makeQuery(id+"F6.opPattern","COPY",BODY,{"derivedFrom":makeQuery(id+"F5.opPattern","COPY",BODY,{"derivedFrom":makeQuery(id+"F2.opPattern","COPY",BODY,{"derivedFrom":makeQuery(id+"F1.opRevolve","SWEPT_BODY",BODY,{"disambiguationData":[OSD([sQuery(id+"F0.wireOp",EDGE,"E1")])]}),"instanceName":"1"}),"instanceName":"1"}),"instanceName":"1"}),"instanceName":"1"}),"instanceName":"1"}),"instanceName":"1"}),"instanceName":"1"});
            var Q2011;
            Q2011=makeQuery(id+"F13.opPattern","COPY",BODY,{"derivedFrom":makeQuery(id+"F11.opPattern","COPY",BODY,{"derivedFrom":makeQuery(id+"F8.opPattern","COPY",BODY,{"derivedFrom":makeQuery(id+"F7.opPattern","COPY",BODY,{"derivedFrom":makeQuery(id+"F6.opPattern","COPY",BODY,{"derivedFrom":makeQuery(id+"F5.opPattern","COPY",BODY,{"derivedFrom":makeQuery(id+"F3.opPattern","COPY",BODY,{"derivedFrom":makeQuery(id+"F2.opPattern","COPY",BODY,{"derivedFrom":makeQuery(id+"F1.opRevolve","SWEPT_BODY",BODY,{"disambiguationData":[OSD([sQuery(id+"F0.wireOp",EDGE,"E1")])]}),"instanceName":"1"}),"instanceName":"1"}),"instanceName":"1"}),"instanceName":"1"}),"instanceName":"1"}),"instanceName":"1"}),"instanceName":"1"}),"instanceName":"1"});
            var Q2012;
            Q2012=makeQuery(id+"F13.opPattern","COPY",BODY,{"derivedFrom":makeQuery(id+"F11.opPattern","COPY",BODY,{"derivedFrom":makeQuery(id+"F8.opPattern","COPY",BODY,{"derivedFrom":makeQuery(id+"F7.opPattern","COPY",BODY,{"derivedFrom":makeQuery(id+"F6.opPattern","COPY",BODY,{"derivedFrom":makeQuery(id+"F5.opPattern","COPY",BODY,{"derivedFrom":makeQuery(id+"F4.opPattern","COPY",BODY,{"derivedFrom":makeQuery(id+"F1.opRevolve","SWEPT_BODY",BODY,{"disambiguationData":[OSD([sQuery(id+"F0.wireOp",EDGE,"E1")])]}),"instanceName":"1"}),"instanceName":"1"}),"instanceName":"1"}),"instanceName":"1"}),"instanceName":"1"}),"instanceName":"1"}),"instanceName":"1"});
            var Q2013;
            Q2013=makeQuery(id+"F13.opPattern","COPY",BODY,{"derivedFrom":makeQuery(id+"F11.opPattern","COPY",BODY,{"derivedFrom":makeQuery(id+"F8.opPattern","COPY",BODY,{"derivedFrom":makeQuery(id+"F7.opPattern","COPY",BODY,{"derivedFrom":makeQuery(id+"F6.opPattern","COPY",BODY,{"derivedFrom":makeQuery(id+"F5.opPattern","COPY",BODY,{"derivedFrom":makeQuery(id+"F4.opPattern","COPY",BODY,{"derivedFrom":makeQuery(id+"F2.opPattern","COPY",BODY,{"derivedFrom":makeQuery(id+"F1.opRevolve","SWEPT_BODY",BODY,{"disambiguationData":[OSD([sQuery(id+"F0.wireOp",EDGE,"E1")])]}),"instanceName":"1"}),"instanceName":"1"}),"instanceName":"1"}),"instanceName":"1"}),"instanceName":"1"}),"instanceName":"1"}),"instanceName":"1"}),"instanceName":"1"});
            var Q2014;
            Q2014=makeQuery(id+"F13.opPattern","COPY",BODY,{"derivedFrom":makeQuery(id+"F11.opPattern","COPY",BODY,{"derivedFrom":makeQuery(id+"F8.opPattern","COPY",BODY,{"derivedFrom":makeQuery(id+"F7.opPattern","COPY",BODY,{"derivedFrom":makeQuery(id+"F6.opPattern","COPY",BODY,{"derivedFrom":makeQuery(id+"F5.opPattern","COPY",BODY,{"derivedFrom":makeQuery(id+"F4.opPattern","COPY",BODY,{"derivedFrom":makeQuery(id+"F3.opPattern","COPY",BODY,{"derivedFrom":makeQuery(id+"F2.opPattern","COPY",BODY,{"derivedFrom":makeQuery(id+"F1.opRevolve","SWEPT_BODY",BODY,{"disambiguationData":[OSD([sQuery(id+"F0.wireOp",EDGE,"E1")])]}),"instanceName":"1"}),"instanceName":"1"}),"instanceName":"1"}),"instanceName":"1"}),"instanceName":"1"}),"instanceName":"1"}),"instanceName":"1"}),"instanceName":"1"}),"instanceName":"1"});
            var Q2015;
            Q2015=makeQuery(id+"F13.opPattern","COPY",BODY,{"derivedFrom":makeQuery(id+"F11.opPattern","COPY",BODY,{"derivedFrom":makeQuery(id+"F9.opPattern","COPY",BODY,{"derivedFrom":makeQuery(id+"F1.opRevolve","SWEPT_BODY",BODY,{"disambiguationData":[OSD([sQuery(id+"F0.wireOp",EDGE,"E1")])]}),"instanceName":"1"}),"instanceName":"1"}),"instanceName":"1"});
            var Q2016;
            Q2016=makeQuery(id+"F13.opPattern","COPY",BODY,{"derivedFrom":makeQuery(id+"F11.opPattern","COPY",BODY,{"derivedFrom":makeQuery(id+"F9.opPattern","COPY",BODY,{"derivedFrom":makeQuery(id+"F2.opPattern","COPY",BODY,{"derivedFrom":makeQuery(id+"F1.opRevolve","SWEPT_BODY",BODY,{"disambiguationData":[OSD([sQuery(id+"F0.wireOp",EDGE,"E1")])]}),"instanceName":"1"}),"instanceName":"1"}),"instanceName":"1"}),"instanceName":"1"});
            var Q2017;
            Q2017=makeQuery(id+"F13.opPattern","COPY",BODY,{"derivedFrom":makeQuery(id+"F11.opPattern","COPY",BODY,{"derivedFrom":makeQuery(id+"F9.opPattern","COPY",BODY,{"derivedFrom":makeQuery(id+"F3.opPattern","COPY",BODY,{"derivedFrom":makeQuery(id+"F2.opPattern","COPY",BODY,{"derivedFrom":makeQuery(id+"F1.opRevolve","SWEPT_BODY",BODY,{"disambiguationData":[OSD([sQuery(id+"F0.wireOp",EDGE,"E1")])]}),"instanceName":"1"}),"instanceName":"1"}),"instanceName":"1"}),"instanceName":"1"}),"instanceName":"1"});
            var Q2018;
            Q2018=makeQuery(id+"F13.opPattern","COPY",BODY,{"derivedFrom":makeQuery(id+"F11.opPattern","COPY",BODY,{"derivedFrom":makeQuery(id+"F9.opPattern","COPY",BODY,{"derivedFrom":makeQuery(id+"F4.opPattern","COPY",BODY,{"derivedFrom":makeQuery(id+"F1.opRevolve","SWEPT_BODY",BODY,{"disambiguationData":[OSD([sQuery(id+"F0.wireOp",EDGE,"E1")])]}),"instanceName":"1"}),"instanceName":"1"}),"instanceName":"1"}),"instanceName":"1"});
            var Q2019;
            Q2019=makeQuery(id+"F13.opPattern","COPY",BODY,{"derivedFrom":makeQuery(id+"F11.opPattern","COPY",BODY,{"derivedFrom":makeQuery(id+"F9.opPattern","COPY",BODY,{"derivedFrom":makeQuery(id+"F4.opPattern","COPY",BODY,{"derivedFrom":makeQuery(id+"F2.opPattern","COPY",BODY,{"derivedFrom":makeQuery(id+"F1.opRevolve","SWEPT_BODY",BODY,{"disambiguationData":[OSD([sQuery(id+"F0.wireOp",EDGE,"E1")])]}),"instanceName":"1"}),"instanceName":"1"}),"instanceName":"1"}),"instanceName":"1"}),"instanceName":"1"});
            var Q2020;
            Q2020=makeQuery(id+"F13.opPattern","COPY",BODY,{"derivedFrom":makeQuery(id+"F11.opPattern","COPY",BODY,{"derivedFrom":makeQuery(id+"F9.opPattern","COPY",BODY,{"derivedFrom":makeQuery(id+"F4.opPattern","COPY",BODY,{"derivedFrom":makeQuery(id+"F3.opPattern","COPY",BODY,{"derivedFrom":makeQuery(id+"F2.opPattern","COPY",BODY,{"derivedFrom":makeQuery(id+"F1.opRevolve","SWEPT_BODY",BODY,{"disambiguationData":[OSD([sQuery(id+"F0.wireOp",EDGE,"E1")])]}),"instanceName":"1"}),"instanceName":"1"}),"instanceName":"1"}),"instanceName":"1"}),"instanceName":"1"}),"instanceName":"1"});
            var Q2021;
            Q2021=makeQuery(id+"F13.opPattern","COPY",BODY,{"derivedFrom":makeQuery(id+"F11.opPattern","COPY",BODY,{"derivedFrom":makeQuery(id+"F9.opPattern","COPY",BODY,{"derivedFrom":makeQuery(id+"F5.opPattern","COPY",BODY,{"derivedFrom":makeQuery(id+"F1.opRevolve","SWEPT_BODY",BODY,{"disambiguationData":[OSD([sQuery(id+"F0.wireOp",EDGE,"E1")])]}),"instanceName":"1"}),"instanceName":"1"}),"instanceName":"1"}),"instanceName":"1"});
            var Q2022;
            Q2022=makeQuery(id+"F13.opPattern","COPY",BODY,{"derivedFrom":makeQuery(id+"F11.opPattern","COPY",BODY,{"derivedFrom":makeQuery(id+"F9.opPattern","COPY",BODY,{"derivedFrom":makeQuery(id+"F5.opPattern","COPY",BODY,{"derivedFrom":makeQuery(id+"F2.opPattern","COPY",BODY,{"derivedFrom":makeQuery(id+"F1.opRevolve","SWEPT_BODY",BODY,{"disambiguationData":[OSD([sQuery(id+"F0.wireOp",EDGE,"E1")])]}),"instanceName":"1"}),"instanceName":"1"}),"instanceName":"1"}),"instanceName":"1"}),"instanceName":"1"});
            var Q2023;
            Q2023=makeQuery(id+"F13.opPattern","COPY",BODY,{"derivedFrom":makeQuery(id+"F11.opPattern","COPY",BODY,{"derivedFrom":makeQuery(id+"F9.opPattern","COPY",BODY,{"derivedFrom":makeQuery(id+"F5.opPattern","COPY",BODY,{"derivedFrom":makeQuery(id+"F3.opPattern","COPY",BODY,{"derivedFrom":makeQuery(id+"F2.opPattern","COPY",BODY,{"derivedFrom":makeQuery(id+"F1.opRevolve","SWEPT_BODY",BODY,{"disambiguationData":[OSD([sQuery(id+"F0.wireOp",EDGE,"E1")])]}),"instanceName":"1"}),"instanceName":"1"}),"instanceName":"1"}),"instanceName":"1"}),"instanceName":"1"}),"instanceName":"1"});
            var Q2024;
            Q2024=makeQuery(id+"F13.opPattern","COPY",BODY,{"derivedFrom":makeQuery(id+"F11.opPattern","COPY",BODY,{"derivedFrom":makeQuery(id+"F9.opPattern","COPY",BODY,{"derivedFrom":makeQuery(id+"F5.opPattern","COPY",BODY,{"derivedFrom":makeQuery(id+"F4.opPattern","COPY",BODY,{"derivedFrom":makeQuery(id+"F1.opRevolve","SWEPT_BODY",BODY,{"disambiguationData":[OSD([sQuery(id+"F0.wireOp",EDGE,"E1")])]}),"instanceName":"1"}),"instanceName":"1"}),"instanceName":"1"}),"instanceName":"1"}),"instanceName":"1"});
            var Q2025;
            Q2025=makeQuery(id+"F13.opPattern","COPY",BODY,{"derivedFrom":makeQuery(id+"F11.opPattern","COPY",BODY,{"derivedFrom":makeQuery(id+"F9.opPattern","COPY",BODY,{"derivedFrom":makeQuery(id+"F5.opPattern","COPY",BODY,{"derivedFrom":makeQuery(id+"F4.opPattern","COPY",BODY,{"derivedFrom":makeQuery(id+"F2.opPattern","COPY",BODY,{"derivedFrom":makeQuery(id+"F1.opRevolve","SWEPT_BODY",BODY,{"disambiguationData":[OSD([sQuery(id+"F0.wireOp",EDGE,"E1")])]}),"instanceName":"1"}),"instanceName":"1"}),"instanceName":"1"}),"instanceName":"1"}),"instanceName":"1"}),"instanceName":"1"});
            var Q2026;
            Q2026=makeQuery(id+"F13.opPattern","COPY",BODY,{"derivedFrom":makeQuery(id+"F11.opPattern","COPY",BODY,{"derivedFrom":makeQuery(id+"F9.opPattern","COPY",BODY,{"derivedFrom":makeQuery(id+"F5.opPattern","COPY",BODY,{"derivedFrom":makeQuery(id+"F4.opPattern","COPY",BODY,{"derivedFrom":makeQuery(id+"F3.opPattern","COPY",BODY,{"derivedFrom":makeQuery(id+"F2.opPattern","COPY",BODY,{"derivedFrom":makeQuery(id+"F1.opRevolve","SWEPT_BODY",BODY,{"disambiguationData":[OSD([sQuery(id+"F0.wireOp",EDGE,"E1")])]}),"instanceName":"1"}),"instanceName":"1"}),"instanceName":"1"}),"instanceName":"1"}),"instanceName":"1"}),"instanceName":"1"}),"instanceName":"1"});
            var Q2027;
            Q2027=makeQuery(id+"F13.opPattern","COPY",BODY,{"derivedFrom":makeQuery(id+"F11.opPattern","COPY",BODY,{"derivedFrom":makeQuery(id+"F9.opPattern","COPY",BODY,{"derivedFrom":makeQuery(id+"F6.opPattern","COPY",BODY,{"derivedFrom":makeQuery(id+"F1.opRevolve","SWEPT_BODY",BODY,{"disambiguationData":[OSD([sQuery(id+"F0.wireOp",EDGE,"E1")])]}),"instanceName":"1"}),"instanceName":"1"}),"instanceName":"1"}),"instanceName":"1"});
            var Q2028;
            Q2028=makeQuery(id+"F13.opPattern","COPY",BODY,{"derivedFrom":makeQuery(id+"F11.opPattern","COPY",BODY,{"derivedFrom":makeQuery(id+"F9.opPattern","COPY",BODY,{"derivedFrom":makeQuery(id+"F6.opPattern","COPY",BODY,{"derivedFrom":makeQuery(id+"F2.opPattern","COPY",BODY,{"derivedFrom":makeQuery(id+"F1.opRevolve","SWEPT_BODY",BODY,{"disambiguationData":[OSD([sQuery(id+"F0.wireOp",EDGE,"E1")])]}),"instanceName":"1"}),"instanceName":"1"}),"instanceName":"1"}),"instanceName":"1"}),"instanceName":"1"});
            var Q2029;
            Q2029=makeQuery(id+"F13.opPattern","COPY",BODY,{"derivedFrom":makeQuery(id+"F11.opPattern","COPY",BODY,{"derivedFrom":makeQuery(id+"F9.opPattern","COPY",BODY,{"derivedFrom":makeQuery(id+"F6.opPattern","COPY",BODY,{"derivedFrom":makeQuery(id+"F3.opPattern","COPY",BODY,{"derivedFrom":makeQuery(id+"F2.opPattern","COPY",BODY,{"derivedFrom":makeQuery(id+"F1.opRevolve","SWEPT_BODY",BODY,{"disambiguationData":[OSD([sQuery(id+"F0.wireOp",EDGE,"E1")])]}),"instanceName":"1"}),"instanceName":"1"}),"instanceName":"1"}),"instanceName":"1"}),"instanceName":"1"}),"instanceName":"1"});
            var Q2030;
            Q2030=makeQuery(id+"F13.opPattern","COPY",BODY,{"derivedFrom":makeQuery(id+"F11.opPattern","COPY",BODY,{"derivedFrom":makeQuery(id+"F9.opPattern","COPY",BODY,{"derivedFrom":makeQuery(id+"F6.opPattern","COPY",BODY,{"derivedFrom":makeQuery(id+"F4.opPattern","COPY",BODY,{"derivedFrom":makeQuery(id+"F1.opRevolve","SWEPT_BODY",BODY,{"disambiguationData":[OSD([sQuery(id+"F0.wireOp",EDGE,"E1")])]}),"instanceName":"1"}),"instanceName":"1"}),"instanceName":"1"}),"instanceName":"1"}),"instanceName":"1"});
            var Q2031;
            Q2031=makeQuery(id+"F13.opPattern","COPY",BODY,{"derivedFrom":makeQuery(id+"F11.opPattern","COPY",BODY,{"derivedFrom":makeQuery(id+"F9.opPattern","COPY",BODY,{"derivedFrom":makeQuery(id+"F6.opPattern","COPY",BODY,{"derivedFrom":makeQuery(id+"F4.opPattern","COPY",BODY,{"derivedFrom":makeQuery(id+"F2.opPattern","COPY",BODY,{"derivedFrom":makeQuery(id+"F1.opRevolve","SWEPT_BODY",BODY,{"disambiguationData":[OSD([sQuery(id+"F0.wireOp",EDGE,"E1")])]}),"instanceName":"1"}),"instanceName":"1"}),"instanceName":"1"}),"instanceName":"1"}),"instanceName":"1"}),"instanceName":"1"});
            var Q2032;
            Q2032=makeQuery(id+"F13.opPattern","COPY",BODY,{"derivedFrom":makeQuery(id+"F11.opPattern","COPY",BODY,{"derivedFrom":makeQuery(id+"F9.opPattern","COPY",BODY,{"derivedFrom":makeQuery(id+"F6.opPattern","COPY",BODY,{"derivedFrom":makeQuery(id+"F4.opPattern","COPY",BODY,{"derivedFrom":makeQuery(id+"F3.opPattern","COPY",BODY,{"derivedFrom":makeQuery(id+"F2.opPattern","COPY",BODY,{"derivedFrom":makeQuery(id+"F1.opRevolve","SWEPT_BODY",BODY,{"disambiguationData":[OSD([sQuery(id+"F0.wireOp",EDGE,"E1")])]}),"instanceName":"1"}),"instanceName":"1"}),"instanceName":"1"}),"instanceName":"1"}),"instanceName":"1"}),"instanceName":"1"}),"instanceName":"1"});
            var Q2033;
            Q2033=makeQuery(id+"F13.opPattern","COPY",BODY,{"derivedFrom":makeQuery(id+"F11.opPattern","COPY",BODY,{"derivedFrom":makeQuery(id+"F9.opPattern","COPY",BODY,{"derivedFrom":makeQuery(id+"F6.opPattern","COPY",BODY,{"derivedFrom":makeQuery(id+"F5.opPattern","COPY",BODY,{"derivedFrom":makeQuery(id+"F1.opRevolve","SWEPT_BODY",BODY,{"disambiguationData":[OSD([sQuery(id+"F0.wireOp",EDGE,"E1")])]}),"instanceName":"1"}),"instanceName":"1"}),"instanceName":"1"}),"instanceName":"1"}),"instanceName":"1"});
            var Q2034;
            Q2034=makeQuery(id+"F13.opPattern","COPY",BODY,{"derivedFrom":makeQuery(id+"F11.opPattern","COPY",BODY,{"derivedFrom":makeQuery(id+"F9.opPattern","COPY",BODY,{"derivedFrom":makeQuery(id+"F6.opPattern","COPY",BODY,{"derivedFrom":makeQuery(id+"F5.opPattern","COPY",BODY,{"derivedFrom":makeQuery(id+"F2.opPattern","COPY",BODY,{"derivedFrom":makeQuery(id+"F1.opRevolve","SWEPT_BODY",BODY,{"disambiguationData":[OSD([sQuery(id+"F0.wireOp",EDGE,"E1")])]}),"instanceName":"1"}),"instanceName":"1"}),"instanceName":"1"}),"instanceName":"1"}),"instanceName":"1"}),"instanceName":"1"});
            var Q2035;
            Q2035=makeQuery(id+"F13.opPattern","COPY",BODY,{"derivedFrom":makeQuery(id+"F11.opPattern","COPY",BODY,{"derivedFrom":makeQuery(id+"F9.opPattern","COPY",BODY,{"derivedFrom":makeQuery(id+"F6.opPattern","COPY",BODY,{"derivedFrom":makeQuery(id+"F5.opPattern","COPY",BODY,{"derivedFrom":makeQuery(id+"F3.opPattern","COPY",BODY,{"derivedFrom":makeQuery(id+"F2.opPattern","COPY",BODY,{"derivedFrom":makeQuery(id+"F1.opRevolve","SWEPT_BODY",BODY,{"disambiguationData":[OSD([sQuery(id+"F0.wireOp",EDGE,"E1")])]}),"instanceName":"1"}),"instanceName":"1"}),"instanceName":"1"}),"instanceName":"1"}),"instanceName":"1"}),"instanceName":"1"}),"instanceName":"1"});
            var Q2036;
            Q2036=makeQuery(id+"F13.opPattern","COPY",BODY,{"derivedFrom":makeQuery(id+"F11.opPattern","COPY",BODY,{"derivedFrom":makeQuery(id+"F9.opPattern","COPY",BODY,{"derivedFrom":makeQuery(id+"F6.opPattern","COPY",BODY,{"derivedFrom":makeQuery(id+"F5.opPattern","COPY",BODY,{"derivedFrom":makeQuery(id+"F4.opPattern","COPY",BODY,{"derivedFrom":makeQuery(id+"F1.opRevolve","SWEPT_BODY",BODY,{"disambiguationData":[OSD([sQuery(id+"F0.wireOp",EDGE,"E1")])]}),"instanceName":"1"}),"instanceName":"1"}),"instanceName":"1"}),"instanceName":"1"}),"instanceName":"1"}),"instanceName":"1"});
            var Q2037;
            Q2037=makeQuery(id+"F13.opPattern","COPY",BODY,{"derivedFrom":makeQuery(id+"F11.opPattern","COPY",BODY,{"derivedFrom":makeQuery(id+"F9.opPattern","COPY",BODY,{"derivedFrom":makeQuery(id+"F6.opPattern","COPY",BODY,{"derivedFrom":makeQuery(id+"F5.opPattern","COPY",BODY,{"derivedFrom":makeQuery(id+"F4.opPattern","COPY",BODY,{"derivedFrom":makeQuery(id+"F2.opPattern","COPY",BODY,{"derivedFrom":makeQuery(id+"F1.opRevolve","SWEPT_BODY",BODY,{"disambiguationData":[OSD([sQuery(id+"F0.wireOp",EDGE,"E1")])]}),"instanceName":"1"}),"instanceName":"1"}),"instanceName":"1"}),"instanceName":"1"}),"instanceName":"1"}),"instanceName":"1"}),"instanceName":"1"});
            var Q2038;
            Q2038=makeQuery(id+"F13.opPattern","COPY",BODY,{"derivedFrom":makeQuery(id+"F11.opPattern","COPY",BODY,{"derivedFrom":makeQuery(id+"F9.opPattern","COPY",BODY,{"derivedFrom":makeQuery(id+"F6.opPattern","COPY",BODY,{"derivedFrom":makeQuery(id+"F5.opPattern","COPY",BODY,{"derivedFrom":makeQuery(id+"F4.opPattern","COPY",BODY,{"derivedFrom":makeQuery(id+"F3.opPattern","COPY",BODY,{"derivedFrom":makeQuery(id+"F2.opPattern","COPY",BODY,{"derivedFrom":makeQuery(id+"F1.opRevolve","SWEPT_BODY",BODY,{"disambiguationData":[OSD([sQuery(id+"F0.wireOp",EDGE,"E1")])]}),"instanceName":"1"}),"instanceName":"1"}),"instanceName":"1"}),"instanceName":"1"}),"instanceName":"1"}),"instanceName":"1"}),"instanceName":"1"}),"instanceName":"1"});
            var Q2039;
            Q2039=makeQuery(id+"F13.opPattern","COPY",BODY,{"derivedFrom":makeQuery(id+"F11.opPattern","COPY",BODY,{"derivedFrom":makeQuery(id+"F9.opPattern","COPY",BODY,{"derivedFrom":makeQuery(id+"F7.opPattern","COPY",BODY,{"derivedFrom":makeQuery(id+"F1.opRevolve","SWEPT_BODY",BODY,{"disambiguationData":[OSD([sQuery(id+"F0.wireOp",EDGE,"E1")])]}),"instanceName":"1"}),"instanceName":"1"}),"instanceName":"1"}),"instanceName":"1"});
            var Q2040;
            Q2040=makeQuery(id+"F13.opPattern","COPY",BODY,{"derivedFrom":makeQuery(id+"F11.opPattern","COPY",BODY,{"derivedFrom":makeQuery(id+"F9.opPattern","COPY",BODY,{"derivedFrom":makeQuery(id+"F7.opPattern","COPY",BODY,{"derivedFrom":makeQuery(id+"F2.opPattern","COPY",BODY,{"derivedFrom":makeQuery(id+"F1.opRevolve","SWEPT_BODY",BODY,{"disambiguationData":[OSD([sQuery(id+"F0.wireOp",EDGE,"E1")])]}),"instanceName":"1"}),"instanceName":"1"}),"instanceName":"1"}),"instanceName":"1"}),"instanceName":"1"});
            var Q2041;
            Q2041=makeQuery(id+"F13.opPattern","COPY",BODY,{"derivedFrom":makeQuery(id+"F11.opPattern","COPY",BODY,{"derivedFrom":makeQuery(id+"F9.opPattern","COPY",BODY,{"derivedFrom":makeQuery(id+"F7.opPattern","COPY",BODY,{"derivedFrom":makeQuery(id+"F3.opPattern","COPY",BODY,{"derivedFrom":makeQuery(id+"F2.opPattern","COPY",BODY,{"derivedFrom":makeQuery(id+"F1.opRevolve","SWEPT_BODY",BODY,{"disambiguationData":[OSD([sQuery(id+"F0.wireOp",EDGE,"E1")])]}),"instanceName":"1"}),"instanceName":"1"}),"instanceName":"1"}),"instanceName":"1"}),"instanceName":"1"}),"instanceName":"1"});
            var Q2042;
            Q2042=makeQuery(id+"F13.opPattern","COPY",BODY,{"derivedFrom":makeQuery(id+"F11.opPattern","COPY",BODY,{"derivedFrom":makeQuery(id+"F9.opPattern","COPY",BODY,{"derivedFrom":makeQuery(id+"F7.opPattern","COPY",BODY,{"derivedFrom":makeQuery(id+"F4.opPattern","COPY",BODY,{"derivedFrom":makeQuery(id+"F1.opRevolve","SWEPT_BODY",BODY,{"disambiguationData":[OSD([sQuery(id+"F0.wireOp",EDGE,"E1")])]}),"instanceName":"1"}),"instanceName":"1"}),"instanceName":"1"}),"instanceName":"1"}),"instanceName":"1"});
            var Q2043;
            Q2043=makeQuery(id+"F13.opPattern","COPY",BODY,{"derivedFrom":makeQuery(id+"F11.opPattern","COPY",BODY,{"derivedFrom":makeQuery(id+"F9.opPattern","COPY",BODY,{"derivedFrom":makeQuery(id+"F7.opPattern","COPY",BODY,{"derivedFrom":makeQuery(id+"F4.opPattern","COPY",BODY,{"derivedFrom":makeQuery(id+"F2.opPattern","COPY",BODY,{"derivedFrom":makeQuery(id+"F1.opRevolve","SWEPT_BODY",BODY,{"disambiguationData":[OSD([sQuery(id+"F0.wireOp",EDGE,"E1")])]}),"instanceName":"1"}),"instanceName":"1"}),"instanceName":"1"}),"instanceName":"1"}),"instanceName":"1"}),"instanceName":"1"});
            var Q2044;
            Q2044=makeQuery(id+"F13.opPattern","COPY",BODY,{"derivedFrom":makeQuery(id+"F11.opPattern","COPY",BODY,{"derivedFrom":makeQuery(id+"F9.opPattern","COPY",BODY,{"derivedFrom":makeQuery(id+"F7.opPattern","COPY",BODY,{"derivedFrom":makeQuery(id+"F4.opPattern","COPY",BODY,{"derivedFrom":makeQuery(id+"F3.opPattern","COPY",BODY,{"derivedFrom":makeQuery(id+"F2.opPattern","COPY",BODY,{"derivedFrom":makeQuery(id+"F1.opRevolve","SWEPT_BODY",BODY,{"disambiguationData":[OSD([sQuery(id+"F0.wireOp",EDGE,"E1")])]}),"instanceName":"1"}),"instanceName":"1"}),"instanceName":"1"}),"instanceName":"1"}),"instanceName":"1"}),"instanceName":"1"}),"instanceName":"1"});
            var Q2045;
            Q2045=makeQuery(id+"F13.opPattern","COPY",BODY,{"derivedFrom":makeQuery(id+"F11.opPattern","COPY",BODY,{"derivedFrom":makeQuery(id+"F9.opPattern","COPY",BODY,{"derivedFrom":makeQuery(id+"F7.opPattern","COPY",BODY,{"derivedFrom":makeQuery(id+"F5.opPattern","COPY",BODY,{"derivedFrom":makeQuery(id+"F1.opRevolve","SWEPT_BODY",BODY,{"disambiguationData":[OSD([sQuery(id+"F0.wireOp",EDGE,"E1")])]}),"instanceName":"1"}),"instanceName":"1"}),"instanceName":"1"}),"instanceName":"1"}),"instanceName":"1"});
            var Q2046;
            Q2046=makeQuery(id+"F13.opPattern","COPY",BODY,{"derivedFrom":makeQuery(id+"F11.opPattern","COPY",BODY,{"derivedFrom":makeQuery(id+"F9.opPattern","COPY",BODY,{"derivedFrom":makeQuery(id+"F7.opPattern","COPY",BODY,{"derivedFrom":makeQuery(id+"F5.opPattern","COPY",BODY,{"derivedFrom":makeQuery(id+"F2.opPattern","COPY",BODY,{"derivedFrom":makeQuery(id+"F1.opRevolve","SWEPT_BODY",BODY,{"disambiguationData":[OSD([sQuery(id+"F0.wireOp",EDGE,"E1")])]}),"instanceName":"1"}),"instanceName":"1"}),"instanceName":"1"}),"instanceName":"1"}),"instanceName":"1"}),"instanceName":"1"});
            var Q2047;
            Q2047=makeQuery(id+"F13.opPattern","COPY",BODY,{"derivedFrom":makeQuery(id+"F11.opPattern","COPY",BODY,{"derivedFrom":makeQuery(id+"F9.opPattern","COPY",BODY,{"derivedFrom":makeQuery(id+"F7.opPattern","COPY",BODY,{"derivedFrom":makeQuery(id+"F5.opPattern","COPY",BODY,{"derivedFrom":makeQuery(id+"F3.opPattern","COPY",BODY,{"derivedFrom":makeQuery(id+"F2.opPattern","COPY",BODY,{"derivedFrom":makeQuery(id+"F1.opRevolve","SWEPT_BODY",BODY,{"disambiguationData":[OSD([sQuery(id+"F0.wireOp",EDGE,"E1")])]}),"instanceName":"1"}),"instanceName":"1"}),"instanceName":"1"}),"instanceName":"1"}),"instanceName":"1"}),"instanceName":"1"}),"instanceName":"1"});
            var Q2048;
            Q2048=makeQuery(id+"F13.opPattern","COPY",BODY,{"derivedFrom":makeQuery(id+"F11.opPattern","COPY",BODY,{"derivedFrom":makeQuery(id+"F9.opPattern","COPY",BODY,{"derivedFrom":makeQuery(id+"F7.opPattern","COPY",BODY,{"derivedFrom":makeQuery(id+"F5.opPattern","COPY",BODY,{"derivedFrom":makeQuery(id+"F4.opPattern","COPY",BODY,{"derivedFrom":makeQuery(id+"F1.opRevolve","SWEPT_BODY",BODY,{"disambiguationData":[OSD([sQuery(id+"F0.wireOp",EDGE,"E1")])]}),"instanceName":"1"}),"instanceName":"1"}),"instanceName":"1"}),"instanceName":"1"}),"instanceName":"1"}),"instanceName":"1"});
            var Q2049;
            Q2049=makeQuery(id+"F13.opPattern","COPY",BODY,{"derivedFrom":makeQuery(id+"F11.opPattern","COPY",BODY,{"derivedFrom":makeQuery(id+"F9.opPattern","COPY",BODY,{"derivedFrom":makeQuery(id+"F7.opPattern","COPY",BODY,{"derivedFrom":makeQuery(id+"F5.opPattern","COPY",BODY,{"derivedFrom":makeQuery(id+"F4.opPattern","COPY",BODY,{"derivedFrom":makeQuery(id+"F2.opPattern","COPY",BODY,{"derivedFrom":makeQuery(id+"F1.opRevolve","SWEPT_BODY",BODY,{"disambiguationData":[OSD([sQuery(id+"F0.wireOp",EDGE,"E1")])]}),"instanceName":"1"}),"instanceName":"1"}),"instanceName":"1"}),"instanceName":"1"}),"instanceName":"1"}),"instanceName":"1"}),"instanceName":"1"});
            var Q2050;
            Q2050=makeQuery(id+"F13.opPattern","COPY",BODY,{"derivedFrom":makeQuery(id+"F11.opPattern","COPY",BODY,{"derivedFrom":makeQuery(id+"F9.opPattern","COPY",BODY,{"derivedFrom":makeQuery(id+"F7.opPattern","COPY",BODY,{"derivedFrom":makeQuery(id+"F5.opPattern","COPY",BODY,{"derivedFrom":makeQuery(id+"F4.opPattern","COPY",BODY,{"derivedFrom":makeQuery(id+"F3.opPattern","COPY",BODY,{"derivedFrom":makeQuery(id+"F2.opPattern","COPY",BODY,{"derivedFrom":makeQuery(id+"F1.opRevolve","SWEPT_BODY",BODY,{"disambiguationData":[OSD([sQuery(id+"F0.wireOp",EDGE,"E1")])]}),"instanceName":"1"}),"instanceName":"1"}),"instanceName":"1"}),"instanceName":"1"}),"instanceName":"1"}),"instanceName":"1"}),"instanceName":"1"}),"instanceName":"1"});
            var Q2051;
            Q2051=makeQuery(id+"F13.opPattern","COPY",BODY,{"derivedFrom":makeQuery(id+"F11.opPattern","COPY",BODY,{"derivedFrom":makeQuery(id+"F9.opPattern","COPY",BODY,{"derivedFrom":makeQuery(id+"F7.opPattern","COPY",BODY,{"derivedFrom":makeQuery(id+"F6.opPattern","COPY",BODY,{"derivedFrom":makeQuery(id+"F1.opRevolve","SWEPT_BODY",BODY,{"disambiguationData":[OSD([sQuery(id+"F0.wireOp",EDGE,"E1")])]}),"instanceName":"1"}),"instanceName":"1"}),"instanceName":"1"}),"instanceName":"1"}),"instanceName":"1"});
            var Q2052;
            Q2052=makeQuery(id+"F13.opPattern","COPY",BODY,{"derivedFrom":makeQuery(id+"F11.opPattern","COPY",BODY,{"derivedFrom":makeQuery(id+"F9.opPattern","COPY",BODY,{"derivedFrom":makeQuery(id+"F7.opPattern","COPY",BODY,{"derivedFrom":makeQuery(id+"F6.opPattern","COPY",BODY,{"derivedFrom":makeQuery(id+"F2.opPattern","COPY",BODY,{"derivedFrom":makeQuery(id+"F1.opRevolve","SWEPT_BODY",BODY,{"disambiguationData":[OSD([sQuery(id+"F0.wireOp",EDGE,"E1")])]}),"instanceName":"1"}),"instanceName":"1"}),"instanceName":"1"}),"instanceName":"1"}),"instanceName":"1"}),"instanceName":"1"});
            var Q2053;
            Q2053=makeQuery(id+"F13.opPattern","COPY",BODY,{"derivedFrom":makeQuery(id+"F11.opPattern","COPY",BODY,{"derivedFrom":makeQuery(id+"F9.opPattern","COPY",BODY,{"derivedFrom":makeQuery(id+"F7.opPattern","COPY",BODY,{"derivedFrom":makeQuery(id+"F6.opPattern","COPY",BODY,{"derivedFrom":makeQuery(id+"F3.opPattern","COPY",BODY,{"derivedFrom":makeQuery(id+"F2.opPattern","COPY",BODY,{"derivedFrom":makeQuery(id+"F1.opRevolve","SWEPT_BODY",BODY,{"disambiguationData":[OSD([sQuery(id+"F0.wireOp",EDGE,"E1")])]}),"instanceName":"1"}),"instanceName":"1"}),"instanceName":"1"}),"instanceName":"1"}),"instanceName":"1"}),"instanceName":"1"}),"instanceName":"1"});
            var Q2054;
            Q2054=makeQuery(id+"F13.opPattern","COPY",BODY,{"derivedFrom":makeQuery(id+"F11.opPattern","COPY",BODY,{"derivedFrom":makeQuery(id+"F9.opPattern","COPY",BODY,{"derivedFrom":makeQuery(id+"F7.opPattern","COPY",BODY,{"derivedFrom":makeQuery(id+"F6.opPattern","COPY",BODY,{"derivedFrom":makeQuery(id+"F4.opPattern","COPY",BODY,{"derivedFrom":makeQuery(id+"F1.opRevolve","SWEPT_BODY",BODY,{"disambiguationData":[OSD([sQuery(id+"F0.wireOp",EDGE,"E1")])]}),"instanceName":"1"}),"instanceName":"1"}),"instanceName":"1"}),"instanceName":"1"}),"instanceName":"1"}),"instanceName":"1"});
            var Q2055;
            Q2055=makeQuery(id+"F13.opPattern","COPY",BODY,{"derivedFrom":makeQuery(id+"F11.opPattern","COPY",BODY,{"derivedFrom":makeQuery(id+"F9.opPattern","COPY",BODY,{"derivedFrom":makeQuery(id+"F7.opPattern","COPY",BODY,{"derivedFrom":makeQuery(id+"F6.opPattern","COPY",BODY,{"derivedFrom":makeQuery(id+"F4.opPattern","COPY",BODY,{"derivedFrom":makeQuery(id+"F2.opPattern","COPY",BODY,{"derivedFrom":makeQuery(id+"F1.opRevolve","SWEPT_BODY",BODY,{"disambiguationData":[OSD([sQuery(id+"F0.wireOp",EDGE,"E1")])]}),"instanceName":"1"}),"instanceName":"1"}),"instanceName":"1"}),"instanceName":"1"}),"instanceName":"1"}),"instanceName":"1"}),"instanceName":"1"});
            var Q2056;
            Q2056=makeQuery(id+"F13.opPattern","COPY",BODY,{"derivedFrom":makeQuery(id+"F11.opPattern","COPY",BODY,{"derivedFrom":makeQuery(id+"F9.opPattern","COPY",BODY,{"derivedFrom":makeQuery(id+"F7.opPattern","COPY",BODY,{"derivedFrom":makeQuery(id+"F6.opPattern","COPY",BODY,{"derivedFrom":makeQuery(id+"F4.opPattern","COPY",BODY,{"derivedFrom":makeQuery(id+"F3.opPattern","COPY",BODY,{"derivedFrom":makeQuery(id+"F2.opPattern","COPY",BODY,{"derivedFrom":makeQuery(id+"F1.opRevolve","SWEPT_BODY",BODY,{"disambiguationData":[OSD([sQuery(id+"F0.wireOp",EDGE,"E1")])]}),"instanceName":"1"}),"instanceName":"1"}),"instanceName":"1"}),"instanceName":"1"}),"instanceName":"1"}),"instanceName":"1"}),"instanceName":"1"}),"instanceName":"1"});
            var Q2057;
            Q2057=makeQuery(id+"F13.opPattern","COPY",BODY,{"derivedFrom":makeQuery(id+"F11.opPattern","COPY",BODY,{"derivedFrom":makeQuery(id+"F9.opPattern","COPY",BODY,{"derivedFrom":makeQuery(id+"F7.opPattern","COPY",BODY,{"derivedFrom":makeQuery(id+"F6.opPattern","COPY",BODY,{"derivedFrom":makeQuery(id+"F5.opPattern","COPY",BODY,{"derivedFrom":makeQuery(id+"F1.opRevolve","SWEPT_BODY",BODY,{"disambiguationData":[OSD([sQuery(id+"F0.wireOp",EDGE,"E1")])]}),"instanceName":"1"}),"instanceName":"1"}),"instanceName":"1"}),"instanceName":"1"}),"instanceName":"1"}),"instanceName":"1"});
            var Q2058;
            Q2058=makeQuery(id+"F13.opPattern","COPY",BODY,{"derivedFrom":makeQuery(id+"F11.opPattern","COPY",BODY,{"derivedFrom":makeQuery(id+"F9.opPattern","COPY",BODY,{"derivedFrom":makeQuery(id+"F7.opPattern","COPY",BODY,{"derivedFrom":makeQuery(id+"F6.opPattern","COPY",BODY,{"derivedFrom":makeQuery(id+"F5.opPattern","COPY",BODY,{"derivedFrom":makeQuery(id+"F2.opPattern","COPY",BODY,{"derivedFrom":makeQuery(id+"F1.opRevolve","SWEPT_BODY",BODY,{"disambiguationData":[OSD([sQuery(id+"F0.wireOp",EDGE,"E1")])]}),"instanceName":"1"}),"instanceName":"1"}),"instanceName":"1"}),"instanceName":"1"}),"instanceName":"1"}),"instanceName":"1"}),"instanceName":"1"});
            var Q2059;
            Q2059=makeQuery(id+"F13.opPattern","COPY",BODY,{"derivedFrom":makeQuery(id+"F11.opPattern","COPY",BODY,{"derivedFrom":makeQuery(id+"F9.opPattern","COPY",BODY,{"derivedFrom":makeQuery(id+"F7.opPattern","COPY",BODY,{"derivedFrom":makeQuery(id+"F6.opPattern","COPY",BODY,{"derivedFrom":makeQuery(id+"F5.opPattern","COPY",BODY,{"derivedFrom":makeQuery(id+"F3.opPattern","COPY",BODY,{"derivedFrom":makeQuery(id+"F2.opPattern","COPY",BODY,{"derivedFrom":makeQuery(id+"F1.opRevolve","SWEPT_BODY",BODY,{"disambiguationData":[OSD([sQuery(id+"F0.wireOp",EDGE,"E1")])]}),"instanceName":"1"}),"instanceName":"1"}),"instanceName":"1"}),"instanceName":"1"}),"instanceName":"1"}),"instanceName":"1"}),"instanceName":"1"}),"instanceName":"1"});
            var Q2060;
            Q2060=makeQuery(id+"F13.opPattern","COPY",BODY,{"derivedFrom":makeQuery(id+"F11.opPattern","COPY",BODY,{"derivedFrom":makeQuery(id+"F9.opPattern","COPY",BODY,{"derivedFrom":makeQuery(id+"F7.opPattern","COPY",BODY,{"derivedFrom":makeQuery(id+"F6.opPattern","COPY",BODY,{"derivedFrom":makeQuery(id+"F5.opPattern","COPY",BODY,{"derivedFrom":makeQuery(id+"F4.opPattern","COPY",BODY,{"derivedFrom":makeQuery(id+"F1.opRevolve","SWEPT_BODY",BODY,{"disambiguationData":[OSD([sQuery(id+"F0.wireOp",EDGE,"E1")])]}),"instanceName":"1"}),"instanceName":"1"}),"instanceName":"1"}),"instanceName":"1"}),"instanceName":"1"}),"instanceName":"1"}),"instanceName":"1"});
            var Q2061;
            Q2061=makeQuery(id+"F13.opPattern","COPY",BODY,{"derivedFrom":makeQuery(id+"F11.opPattern","COPY",BODY,{"derivedFrom":makeQuery(id+"F9.opPattern","COPY",BODY,{"derivedFrom":makeQuery(id+"F7.opPattern","COPY",BODY,{"derivedFrom":makeQuery(id+"F6.opPattern","COPY",BODY,{"derivedFrom":makeQuery(id+"F5.opPattern","COPY",BODY,{"derivedFrom":makeQuery(id+"F4.opPattern","COPY",BODY,{"derivedFrom":makeQuery(id+"F2.opPattern","COPY",BODY,{"derivedFrom":makeQuery(id+"F1.opRevolve","SWEPT_BODY",BODY,{"disambiguationData":[OSD([sQuery(id+"F0.wireOp",EDGE,"E1")])]}),"instanceName":"1"}),"instanceName":"1"}),"instanceName":"1"}),"instanceName":"1"}),"instanceName":"1"}),"instanceName":"1"}),"instanceName":"1"}),"instanceName":"1"});
            var Q2062;
            Q2062=makeQuery(id+"F13.opPattern","COPY",BODY,{"derivedFrom":makeQuery(id+"F11.opPattern","COPY",BODY,{"derivedFrom":makeQuery(id+"F9.opPattern","COPY",BODY,{"derivedFrom":makeQuery(id+"F7.opPattern","COPY",BODY,{"derivedFrom":makeQuery(id+"F6.opPattern","COPY",BODY,{"derivedFrom":makeQuery(id+"F5.opPattern","COPY",BODY,{"derivedFrom":makeQuery(id+"F4.opPattern","COPY",BODY,{"derivedFrom":makeQuery(id+"F3.opPattern","COPY",BODY,{"derivedFrom":makeQuery(id+"F2.opPattern","COPY",BODY,{"derivedFrom":makeQuery(id+"F1.opRevolve","SWEPT_BODY",BODY,{"disambiguationData":[OSD([sQuery(id+"F0.wireOp",EDGE,"E1")])]}),"instanceName":"1"}),"instanceName":"1"}),"instanceName":"1"}),"instanceName":"1"}),"instanceName":"1"}),"instanceName":"1"}),"instanceName":"1"}),"instanceName":"1"}),"instanceName":"1"});
            var Q2063;
            Q2063=makeQuery(id+"F13.opPattern","COPY",BODY,{"derivedFrom":makeQuery(id+"F11.opPattern","COPY",BODY,{"derivedFrom":makeQuery(id+"F9.opPattern","COPY",BODY,{"derivedFrom":makeQuery(id+"F8.opPattern","COPY",BODY,{"derivedFrom":makeQuery(id+"F1.opRevolve","SWEPT_BODY",BODY,{"disambiguationData":[OSD([sQuery(id+"F0.wireOp",EDGE,"E1")])]}),"instanceName":"1"}),"instanceName":"1"}),"instanceName":"1"}),"instanceName":"1"});
            var Q2064;
            Q2064=makeQuery(id+"F13.opPattern","COPY",BODY,{"derivedFrom":makeQuery(id+"F11.opPattern","COPY",BODY,{"derivedFrom":makeQuery(id+"F9.opPattern","COPY",BODY,{"derivedFrom":makeQuery(id+"F8.opPattern","COPY",BODY,{"derivedFrom":makeQuery(id+"F2.opPattern","COPY",BODY,{"derivedFrom":makeQuery(id+"F1.opRevolve","SWEPT_BODY",BODY,{"disambiguationData":[OSD([sQuery(id+"F0.wireOp",EDGE,"E1")])]}),"instanceName":"1"}),"instanceName":"1"}),"instanceName":"1"}),"instanceName":"1"}),"instanceName":"1"});
            var Q2065;
            Q2065=makeQuery(id+"F13.opPattern","COPY",BODY,{"derivedFrom":makeQuery(id+"F11.opPattern","COPY",BODY,{"derivedFrom":makeQuery(id+"F9.opPattern","COPY",BODY,{"derivedFrom":makeQuery(id+"F8.opPattern","COPY",BODY,{"derivedFrom":makeQuery(id+"F3.opPattern","COPY",BODY,{"derivedFrom":makeQuery(id+"F2.opPattern","COPY",BODY,{"derivedFrom":makeQuery(id+"F1.opRevolve","SWEPT_BODY",BODY,{"disambiguationData":[OSD([sQuery(id+"F0.wireOp",EDGE,"E1")])]}),"instanceName":"1"}),"instanceName":"1"}),"instanceName":"1"}),"instanceName":"1"}),"instanceName":"1"}),"instanceName":"1"});
            var Q2066;
            Q2066=makeQuery(id+"F13.opPattern","COPY",BODY,{"derivedFrom":makeQuery(id+"F11.opPattern","COPY",BODY,{"derivedFrom":makeQuery(id+"F9.opPattern","COPY",BODY,{"derivedFrom":makeQuery(id+"F8.opPattern","COPY",BODY,{"derivedFrom":makeQuery(id+"F4.opPattern","COPY",BODY,{"derivedFrom":makeQuery(id+"F1.opRevolve","SWEPT_BODY",BODY,{"disambiguationData":[OSD([sQuery(id+"F0.wireOp",EDGE,"E1")])]}),"instanceName":"1"}),"instanceName":"1"}),"instanceName":"1"}),"instanceName":"1"}),"instanceName":"1"});
            var Q2067;
            Q2067=makeQuery(id+"F13.opPattern","COPY",BODY,{"derivedFrom":makeQuery(id+"F11.opPattern","COPY",BODY,{"derivedFrom":makeQuery(id+"F9.opPattern","COPY",BODY,{"derivedFrom":makeQuery(id+"F8.opPattern","COPY",BODY,{"derivedFrom":makeQuery(id+"F4.opPattern","COPY",BODY,{"derivedFrom":makeQuery(id+"F2.opPattern","COPY",BODY,{"derivedFrom":makeQuery(id+"F1.opRevolve","SWEPT_BODY",BODY,{"disambiguationData":[OSD([sQuery(id+"F0.wireOp",EDGE,"E1")])]}),"instanceName":"1"}),"instanceName":"1"}),"instanceName":"1"}),"instanceName":"1"}),"instanceName":"1"}),"instanceName":"1"});
            var Q2068;
            Q2068=makeQuery(id+"F13.opPattern","COPY",BODY,{"derivedFrom":makeQuery(id+"F11.opPattern","COPY",BODY,{"derivedFrom":makeQuery(id+"F9.opPattern","COPY",BODY,{"derivedFrom":makeQuery(id+"F8.opPattern","COPY",BODY,{"derivedFrom":makeQuery(id+"F4.opPattern","COPY",BODY,{"derivedFrom":makeQuery(id+"F3.opPattern","COPY",BODY,{"derivedFrom":makeQuery(id+"F2.opPattern","COPY",BODY,{"derivedFrom":makeQuery(id+"F1.opRevolve","SWEPT_BODY",BODY,{"disambiguationData":[OSD([sQuery(id+"F0.wireOp",EDGE,"E1")])]}),"instanceName":"1"}),"instanceName":"1"}),"instanceName":"1"}),"instanceName":"1"}),"instanceName":"1"}),"instanceName":"1"}),"instanceName":"1"});
            var Q2069;
            Q2069=makeQuery(id+"F13.opPattern","COPY",BODY,{"derivedFrom":makeQuery(id+"F11.opPattern","COPY",BODY,{"derivedFrom":makeQuery(id+"F9.opPattern","COPY",BODY,{"derivedFrom":makeQuery(id+"F8.opPattern","COPY",BODY,{"derivedFrom":makeQuery(id+"F5.opPattern","COPY",BODY,{"derivedFrom":makeQuery(id+"F1.opRevolve","SWEPT_BODY",BODY,{"disambiguationData":[OSD([sQuery(id+"F0.wireOp",EDGE,"E1")])]}),"instanceName":"1"}),"instanceName":"1"}),"instanceName":"1"}),"instanceName":"1"}),"instanceName":"1"});
            var Q2070;
            Q2070=makeQuery(id+"F13.opPattern","COPY",BODY,{"derivedFrom":makeQuery(id+"F11.opPattern","COPY",BODY,{"derivedFrom":makeQuery(id+"F9.opPattern","COPY",BODY,{"derivedFrom":makeQuery(id+"F8.opPattern","COPY",BODY,{"derivedFrom":makeQuery(id+"F5.opPattern","COPY",BODY,{"derivedFrom":makeQuery(id+"F2.opPattern","COPY",BODY,{"derivedFrom":makeQuery(id+"F1.opRevolve","SWEPT_BODY",BODY,{"disambiguationData":[OSD([sQuery(id+"F0.wireOp",EDGE,"E1")])]}),"instanceName":"1"}),"instanceName":"1"}),"instanceName":"1"}),"instanceName":"1"}),"instanceName":"1"}),"instanceName":"1"});
            var Q2071;
            Q2071=makeQuery(id+"F13.opPattern","COPY",BODY,{"derivedFrom":makeQuery(id+"F11.opPattern","COPY",BODY,{"derivedFrom":makeQuery(id+"F9.opPattern","COPY",BODY,{"derivedFrom":makeQuery(id+"F8.opPattern","COPY",BODY,{"derivedFrom":makeQuery(id+"F5.opPattern","COPY",BODY,{"derivedFrom":makeQuery(id+"F3.opPattern","COPY",BODY,{"derivedFrom":makeQuery(id+"F2.opPattern","COPY",BODY,{"derivedFrom":makeQuery(id+"F1.opRevolve","SWEPT_BODY",BODY,{"disambiguationData":[OSD([sQuery(id+"F0.wireOp",EDGE,"E1")])]}),"instanceName":"1"}),"instanceName":"1"}),"instanceName":"1"}),"instanceName":"1"}),"instanceName":"1"}),"instanceName":"1"}),"instanceName":"1"});
            var Q2072;
            Q2072=makeQuery(id+"F13.opPattern","COPY",BODY,{"derivedFrom":makeQuery(id+"F11.opPattern","COPY",BODY,{"derivedFrom":makeQuery(id+"F9.opPattern","COPY",BODY,{"derivedFrom":makeQuery(id+"F8.opPattern","COPY",BODY,{"derivedFrom":makeQuery(id+"F5.opPattern","COPY",BODY,{"derivedFrom":makeQuery(id+"F4.opPattern","COPY",BODY,{"derivedFrom":makeQuery(id+"F1.opRevolve","SWEPT_BODY",BODY,{"disambiguationData":[OSD([sQuery(id+"F0.wireOp",EDGE,"E1")])]}),"instanceName":"1"}),"instanceName":"1"}),"instanceName":"1"}),"instanceName":"1"}),"instanceName":"1"}),"instanceName":"1"});
            var Q2073;
            Q2073=makeQuery(id+"F13.opPattern","COPY",BODY,{"derivedFrom":makeQuery(id+"F11.opPattern","COPY",BODY,{"derivedFrom":makeQuery(id+"F9.opPattern","COPY",BODY,{"derivedFrom":makeQuery(id+"F8.opPattern","COPY",BODY,{"derivedFrom":makeQuery(id+"F5.opPattern","COPY",BODY,{"derivedFrom":makeQuery(id+"F4.opPattern","COPY",BODY,{"derivedFrom":makeQuery(id+"F2.opPattern","COPY",BODY,{"derivedFrom":makeQuery(id+"F1.opRevolve","SWEPT_BODY",BODY,{"disambiguationData":[OSD([sQuery(id+"F0.wireOp",EDGE,"E1")])]}),"instanceName":"1"}),"instanceName":"1"}),"instanceName":"1"}),"instanceName":"1"}),"instanceName":"1"}),"instanceName":"1"}),"instanceName":"1"});
            var Q2074;
            Q2074=makeQuery(id+"F13.opPattern","COPY",BODY,{"derivedFrom":makeQuery(id+"F11.opPattern","COPY",BODY,{"derivedFrom":makeQuery(id+"F9.opPattern","COPY",BODY,{"derivedFrom":makeQuery(id+"F8.opPattern","COPY",BODY,{"derivedFrom":makeQuery(id+"F5.opPattern","COPY",BODY,{"derivedFrom":makeQuery(id+"F4.opPattern","COPY",BODY,{"derivedFrom":makeQuery(id+"F3.opPattern","COPY",BODY,{"derivedFrom":makeQuery(id+"F2.opPattern","COPY",BODY,{"derivedFrom":makeQuery(id+"F1.opRevolve","SWEPT_BODY",BODY,{"disambiguationData":[OSD([sQuery(id+"F0.wireOp",EDGE,"E1")])]}),"instanceName":"1"}),"instanceName":"1"}),"instanceName":"1"}),"instanceName":"1"}),"instanceName":"1"}),"instanceName":"1"}),"instanceName":"1"}),"instanceName":"1"});
            var Q2075;
            Q2075=makeQuery(id+"F13.opPattern","COPY",BODY,{"derivedFrom":makeQuery(id+"F11.opPattern","COPY",BODY,{"derivedFrom":makeQuery(id+"F9.opPattern","COPY",BODY,{"derivedFrom":makeQuery(id+"F8.opPattern","COPY",BODY,{"derivedFrom":makeQuery(id+"F6.opPattern","COPY",BODY,{"derivedFrom":makeQuery(id+"F1.opRevolve","SWEPT_BODY",BODY,{"disambiguationData":[OSD([sQuery(id+"F0.wireOp",EDGE,"E1")])]}),"instanceName":"1"}),"instanceName":"1"}),"instanceName":"1"}),"instanceName":"1"}),"instanceName":"1"});
            var Q2076;
            Q2076=makeQuery(id+"F13.opPattern","COPY",BODY,{"derivedFrom":makeQuery(id+"F11.opPattern","COPY",BODY,{"derivedFrom":makeQuery(id+"F9.opPattern","COPY",BODY,{"derivedFrom":makeQuery(id+"F8.opPattern","COPY",BODY,{"derivedFrom":makeQuery(id+"F6.opPattern","COPY",BODY,{"derivedFrom":makeQuery(id+"F2.opPattern","COPY",BODY,{"derivedFrom":makeQuery(id+"F1.opRevolve","SWEPT_BODY",BODY,{"disambiguationData":[OSD([sQuery(id+"F0.wireOp",EDGE,"E1")])]}),"instanceName":"1"}),"instanceName":"1"}),"instanceName":"1"}),"instanceName":"1"}),"instanceName":"1"}),"instanceName":"1"});
            var Q2077;
            Q2077=makeQuery(id+"F13.opPattern","COPY",BODY,{"derivedFrom":makeQuery(id+"F11.opPattern","COPY",BODY,{"derivedFrom":makeQuery(id+"F9.opPattern","COPY",BODY,{"derivedFrom":makeQuery(id+"F8.opPattern","COPY",BODY,{"derivedFrom":makeQuery(id+"F6.opPattern","COPY",BODY,{"derivedFrom":makeQuery(id+"F3.opPattern","COPY",BODY,{"derivedFrom":makeQuery(id+"F2.opPattern","COPY",BODY,{"derivedFrom":makeQuery(id+"F1.opRevolve","SWEPT_BODY",BODY,{"disambiguationData":[OSD([sQuery(id+"F0.wireOp",EDGE,"E1")])]}),"instanceName":"1"}),"instanceName":"1"}),"instanceName":"1"}),"instanceName":"1"}),"instanceName":"1"}),"instanceName":"1"}),"instanceName":"1"});
            var Q2078;
            Q2078=makeQuery(id+"F13.opPattern","COPY",BODY,{"derivedFrom":makeQuery(id+"F11.opPattern","COPY",BODY,{"derivedFrom":makeQuery(id+"F9.opPattern","COPY",BODY,{"derivedFrom":makeQuery(id+"F8.opPattern","COPY",BODY,{"derivedFrom":makeQuery(id+"F6.opPattern","COPY",BODY,{"derivedFrom":makeQuery(id+"F4.opPattern","COPY",BODY,{"derivedFrom":makeQuery(id+"F1.opRevolve","SWEPT_BODY",BODY,{"disambiguationData":[OSD([sQuery(id+"F0.wireOp",EDGE,"E1")])]}),"instanceName":"1"}),"instanceName":"1"}),"instanceName":"1"}),"instanceName":"1"}),"instanceName":"1"}),"instanceName":"1"});
            var Q2079;
            Q2079=makeQuery(id+"F13.opPattern","COPY",BODY,{"derivedFrom":makeQuery(id+"F11.opPattern","COPY",BODY,{"derivedFrom":makeQuery(id+"F9.opPattern","COPY",BODY,{"derivedFrom":makeQuery(id+"F8.opPattern","COPY",BODY,{"derivedFrom":makeQuery(id+"F6.opPattern","COPY",BODY,{"derivedFrom":makeQuery(id+"F4.opPattern","COPY",BODY,{"derivedFrom":makeQuery(id+"F2.opPattern","COPY",BODY,{"derivedFrom":makeQuery(id+"F1.opRevolve","SWEPT_BODY",BODY,{"disambiguationData":[OSD([sQuery(id+"F0.wireOp",EDGE,"E1")])]}),"instanceName":"1"}),"instanceName":"1"}),"instanceName":"1"}),"instanceName":"1"}),"instanceName":"1"}),"instanceName":"1"}),"instanceName":"1"});
            var Q2080;
            Q2080=makeQuery(id+"F13.opPattern","COPY",BODY,{"derivedFrom":makeQuery(id+"F11.opPattern","COPY",BODY,{"derivedFrom":makeQuery(id+"F9.opPattern","COPY",BODY,{"derivedFrom":makeQuery(id+"F8.opPattern","COPY",BODY,{"derivedFrom":makeQuery(id+"F6.opPattern","COPY",BODY,{"derivedFrom":makeQuery(id+"F4.opPattern","COPY",BODY,{"derivedFrom":makeQuery(id+"F3.opPattern","COPY",BODY,{"derivedFrom":makeQuery(id+"F2.opPattern","COPY",BODY,{"derivedFrom":makeQuery(id+"F1.opRevolve","SWEPT_BODY",BODY,{"disambiguationData":[OSD([sQuery(id+"F0.wireOp",EDGE,"E1")])]}),"instanceName":"1"}),"instanceName":"1"}),"instanceName":"1"}),"instanceName":"1"}),"instanceName":"1"}),"instanceName":"1"}),"instanceName":"1"}),"instanceName":"1"});
            var Q2081;
            Q2081=makeQuery(id+"F13.opPattern","COPY",BODY,{"derivedFrom":makeQuery(id+"F11.opPattern","COPY",BODY,{"derivedFrom":makeQuery(id+"F9.opPattern","COPY",BODY,{"derivedFrom":makeQuery(id+"F8.opPattern","COPY",BODY,{"derivedFrom":makeQuery(id+"F6.opPattern","COPY",BODY,{"derivedFrom":makeQuery(id+"F5.opPattern","COPY",BODY,{"derivedFrom":makeQuery(id+"F1.opRevolve","SWEPT_BODY",BODY,{"disambiguationData":[OSD([sQuery(id+"F0.wireOp",EDGE,"E1")])]}),"instanceName":"1"}),"instanceName":"1"}),"instanceName":"1"}),"instanceName":"1"}),"instanceName":"1"}),"instanceName":"1"});
            var Q2082;
            Q2082=makeQuery(id+"F13.opPattern","COPY",BODY,{"derivedFrom":makeQuery(id+"F11.opPattern","COPY",BODY,{"derivedFrom":makeQuery(id+"F9.opPattern","COPY",BODY,{"derivedFrom":makeQuery(id+"F8.opPattern","COPY",BODY,{"derivedFrom":makeQuery(id+"F6.opPattern","COPY",BODY,{"derivedFrom":makeQuery(id+"F5.opPattern","COPY",BODY,{"derivedFrom":makeQuery(id+"F2.opPattern","COPY",BODY,{"derivedFrom":makeQuery(id+"F1.opRevolve","SWEPT_BODY",BODY,{"disambiguationData":[OSD([sQuery(id+"F0.wireOp",EDGE,"E1")])]}),"instanceName":"1"}),"instanceName":"1"}),"instanceName":"1"}),"instanceName":"1"}),"instanceName":"1"}),"instanceName":"1"}),"instanceName":"1"});
            var Q2083;
            Q2083=makeQuery(id+"F13.opPattern","COPY",BODY,{"derivedFrom":makeQuery(id+"F11.opPattern","COPY",BODY,{"derivedFrom":makeQuery(id+"F9.opPattern","COPY",BODY,{"derivedFrom":makeQuery(id+"F8.opPattern","COPY",BODY,{"derivedFrom":makeQuery(id+"F6.opPattern","COPY",BODY,{"derivedFrom":makeQuery(id+"F5.opPattern","COPY",BODY,{"derivedFrom":makeQuery(id+"F3.opPattern","COPY",BODY,{"derivedFrom":makeQuery(id+"F2.opPattern","COPY",BODY,{"derivedFrom":makeQuery(id+"F1.opRevolve","SWEPT_BODY",BODY,{"disambiguationData":[OSD([sQuery(id+"F0.wireOp",EDGE,"E1")])]}),"instanceName":"1"}),"instanceName":"1"}),"instanceName":"1"}),"instanceName":"1"}),"instanceName":"1"}),"instanceName":"1"}),"instanceName":"1"}),"instanceName":"1"});
            var Q2084;
            Q2084=makeQuery(id+"F13.opPattern","COPY",BODY,{"derivedFrom":makeQuery(id+"F11.opPattern","COPY",BODY,{"derivedFrom":makeQuery(id+"F9.opPattern","COPY",BODY,{"derivedFrom":makeQuery(id+"F8.opPattern","COPY",BODY,{"derivedFrom":makeQuery(id+"F6.opPattern","COPY",BODY,{"derivedFrom":makeQuery(id+"F5.opPattern","COPY",BODY,{"derivedFrom":makeQuery(id+"F4.opPattern","COPY",BODY,{"derivedFrom":makeQuery(id+"F1.opRevolve","SWEPT_BODY",BODY,{"disambiguationData":[OSD([sQuery(id+"F0.wireOp",EDGE,"E1")])]}),"instanceName":"1"}),"instanceName":"1"}),"instanceName":"1"}),"instanceName":"1"}),"instanceName":"1"}),"instanceName":"1"}),"instanceName":"1"});
            var Q2085;
            Q2085=makeQuery(id+"F13.opPattern","COPY",BODY,{"derivedFrom":makeQuery(id+"F11.opPattern","COPY",BODY,{"derivedFrom":makeQuery(id+"F9.opPattern","COPY",BODY,{"derivedFrom":makeQuery(id+"F8.opPattern","COPY",BODY,{"derivedFrom":makeQuery(id+"F6.opPattern","COPY",BODY,{"derivedFrom":makeQuery(id+"F5.opPattern","COPY",BODY,{"derivedFrom":makeQuery(id+"F4.opPattern","COPY",BODY,{"derivedFrom":makeQuery(id+"F2.opPattern","COPY",BODY,{"derivedFrom":makeQuery(id+"F1.opRevolve","SWEPT_BODY",BODY,{"disambiguationData":[OSD([sQuery(id+"F0.wireOp",EDGE,"E1")])]}),"instanceName":"1"}),"instanceName":"1"}),"instanceName":"1"}),"instanceName":"1"}),"instanceName":"1"}),"instanceName":"1"}),"instanceName":"1"}),"instanceName":"1"});
            var Q2086;
            Q2086=makeQuery(id+"F13.opPattern","COPY",BODY,{"derivedFrom":makeQuery(id+"F11.opPattern","COPY",BODY,{"derivedFrom":makeQuery(id+"F9.opPattern","COPY",BODY,{"derivedFrom":makeQuery(id+"F8.opPattern","COPY",BODY,{"derivedFrom":makeQuery(id+"F6.opPattern","COPY",BODY,{"derivedFrom":makeQuery(id+"F5.opPattern","COPY",BODY,{"derivedFrom":makeQuery(id+"F4.opPattern","COPY",BODY,{"derivedFrom":makeQuery(id+"F3.opPattern","COPY",BODY,{"derivedFrom":makeQuery(id+"F2.opPattern","COPY",BODY,{"derivedFrom":makeQuery(id+"F1.opRevolve","SWEPT_BODY",BODY,{"disambiguationData":[OSD([sQuery(id+"F0.wireOp",EDGE,"E1")])]}),"instanceName":"1"}),"instanceName":"1"}),"instanceName":"1"}),"instanceName":"1"}),"instanceName":"1"}),"instanceName":"1"}),"instanceName":"1"}),"instanceName":"1"}),"instanceName":"1"});
            var Q2087;
            Q2087=makeQuery(id+"F13.opPattern","COPY",BODY,{"derivedFrom":makeQuery(id+"F11.opPattern","COPY",BODY,{"derivedFrom":makeQuery(id+"F9.opPattern","COPY",BODY,{"derivedFrom":makeQuery(id+"F8.opPattern","COPY",BODY,{"derivedFrom":makeQuery(id+"F7.opPattern","COPY",BODY,{"derivedFrom":makeQuery(id+"F1.opRevolve","SWEPT_BODY",BODY,{"disambiguationData":[OSD([sQuery(id+"F0.wireOp",EDGE,"E1")])]}),"instanceName":"1"}),"instanceName":"1"}),"instanceName":"1"}),"instanceName":"1"}),"instanceName":"1"});
            var Q2088;
            Q2088=makeQuery(id+"F13.opPattern","COPY",BODY,{"derivedFrom":makeQuery(id+"F11.opPattern","COPY",BODY,{"derivedFrom":makeQuery(id+"F9.opPattern","COPY",BODY,{"derivedFrom":makeQuery(id+"F8.opPattern","COPY",BODY,{"derivedFrom":makeQuery(id+"F7.opPattern","COPY",BODY,{"derivedFrom":makeQuery(id+"F2.opPattern","COPY",BODY,{"derivedFrom":makeQuery(id+"F1.opRevolve","SWEPT_BODY",BODY,{"disambiguationData":[OSD([sQuery(id+"F0.wireOp",EDGE,"E1")])]}),"instanceName":"1"}),"instanceName":"1"}),"instanceName":"1"}),"instanceName":"1"}),"instanceName":"1"}),"instanceName":"1"});
            var Q2089;
            Q2089=makeQuery(id+"F13.opPattern","COPY",BODY,{"derivedFrom":makeQuery(id+"F11.opPattern","COPY",BODY,{"derivedFrom":makeQuery(id+"F9.opPattern","COPY",BODY,{"derivedFrom":makeQuery(id+"F8.opPattern","COPY",BODY,{"derivedFrom":makeQuery(id+"F7.opPattern","COPY",BODY,{"derivedFrom":makeQuery(id+"F3.opPattern","COPY",BODY,{"derivedFrom":makeQuery(id+"F2.opPattern","COPY",BODY,{"derivedFrom":makeQuery(id+"F1.opRevolve","SWEPT_BODY",BODY,{"disambiguationData":[OSD([sQuery(id+"F0.wireOp",EDGE,"E1")])]}),"instanceName":"1"}),"instanceName":"1"}),"instanceName":"1"}),"instanceName":"1"}),"instanceName":"1"}),"instanceName":"1"}),"instanceName":"1"});
            var Q2090;
            Q2090=makeQuery(id+"F13.opPattern","COPY",BODY,{"derivedFrom":makeQuery(id+"F11.opPattern","COPY",BODY,{"derivedFrom":makeQuery(id+"F9.opPattern","COPY",BODY,{"derivedFrom":makeQuery(id+"F8.opPattern","COPY",BODY,{"derivedFrom":makeQuery(id+"F7.opPattern","COPY",BODY,{"derivedFrom":makeQuery(id+"F4.opPattern","COPY",BODY,{"derivedFrom":makeQuery(id+"F1.opRevolve","SWEPT_BODY",BODY,{"disambiguationData":[OSD([sQuery(id+"F0.wireOp",EDGE,"E1")])]}),"instanceName":"1"}),"instanceName":"1"}),"instanceName":"1"}),"instanceName":"1"}),"instanceName":"1"}),"instanceName":"1"});
            var Q2091;
            Q2091=makeQuery(id+"F13.opPattern","COPY",BODY,{"derivedFrom":makeQuery(id+"F11.opPattern","COPY",BODY,{"derivedFrom":makeQuery(id+"F9.opPattern","COPY",BODY,{"derivedFrom":makeQuery(id+"F8.opPattern","COPY",BODY,{"derivedFrom":makeQuery(id+"F7.opPattern","COPY",BODY,{"derivedFrom":makeQuery(id+"F4.opPattern","COPY",BODY,{"derivedFrom":makeQuery(id+"F2.opPattern","COPY",BODY,{"derivedFrom":makeQuery(id+"F1.opRevolve","SWEPT_BODY",BODY,{"disambiguationData":[OSD([sQuery(id+"F0.wireOp",EDGE,"E1")])]}),"instanceName":"1"}),"instanceName":"1"}),"instanceName":"1"}),"instanceName":"1"}),"instanceName":"1"}),"instanceName":"1"}),"instanceName":"1"});
            var Q2092;
            Q2092=makeQuery(id+"F13.opPattern","COPY",BODY,{"derivedFrom":makeQuery(id+"F11.opPattern","COPY",BODY,{"derivedFrom":makeQuery(id+"F9.opPattern","COPY",BODY,{"derivedFrom":makeQuery(id+"F8.opPattern","COPY",BODY,{"derivedFrom":makeQuery(id+"F7.opPattern","COPY",BODY,{"derivedFrom":makeQuery(id+"F4.opPattern","COPY",BODY,{"derivedFrom":makeQuery(id+"F3.opPattern","COPY",BODY,{"derivedFrom":makeQuery(id+"F2.opPattern","COPY",BODY,{"derivedFrom":makeQuery(id+"F1.opRevolve","SWEPT_BODY",BODY,{"disambiguationData":[OSD([sQuery(id+"F0.wireOp",EDGE,"E1")])]}),"instanceName":"1"}),"instanceName":"1"}),"instanceName":"1"}),"instanceName":"1"}),"instanceName":"1"}),"instanceName":"1"}),"instanceName":"1"}),"instanceName":"1"});
            var Q2093;
            Q2093=makeQuery(id+"F13.opPattern","COPY",BODY,{"derivedFrom":makeQuery(id+"F11.opPattern","COPY",BODY,{"derivedFrom":makeQuery(id+"F9.opPattern","COPY",BODY,{"derivedFrom":makeQuery(id+"F8.opPattern","COPY",BODY,{"derivedFrom":makeQuery(id+"F7.opPattern","COPY",BODY,{"derivedFrom":makeQuery(id+"F5.opPattern","COPY",BODY,{"derivedFrom":makeQuery(id+"F1.opRevolve","SWEPT_BODY",BODY,{"disambiguationData":[OSD([sQuery(id+"F0.wireOp",EDGE,"E1")])]}),"instanceName":"1"}),"instanceName":"1"}),"instanceName":"1"}),"instanceName":"1"}),"instanceName":"1"}),"instanceName":"1"});
            var Q2094;
            Q2094=makeQuery(id+"F13.opPattern","COPY",BODY,{"derivedFrom":makeQuery(id+"F11.opPattern","COPY",BODY,{"derivedFrom":makeQuery(id+"F9.opPattern","COPY",BODY,{"derivedFrom":makeQuery(id+"F8.opPattern","COPY",BODY,{"derivedFrom":makeQuery(id+"F7.opPattern","COPY",BODY,{"derivedFrom":makeQuery(id+"F5.opPattern","COPY",BODY,{"derivedFrom":makeQuery(id+"F2.opPattern","COPY",BODY,{"derivedFrom":makeQuery(id+"F1.opRevolve","SWEPT_BODY",BODY,{"disambiguationData":[OSD([sQuery(id+"F0.wireOp",EDGE,"E1")])]}),"instanceName":"1"}),"instanceName":"1"}),"instanceName":"1"}),"instanceName":"1"}),"instanceName":"1"}),"instanceName":"1"}),"instanceName":"1"});
            var Q2095;
            Q2095=makeQuery(id+"F13.opPattern","COPY",BODY,{"derivedFrom":makeQuery(id+"F11.opPattern","COPY",BODY,{"derivedFrom":makeQuery(id+"F9.opPattern","COPY",BODY,{"derivedFrom":makeQuery(id+"F8.opPattern","COPY",BODY,{"derivedFrom":makeQuery(id+"F7.opPattern","COPY",BODY,{"derivedFrom":makeQuery(id+"F5.opPattern","COPY",BODY,{"derivedFrom":makeQuery(id+"F3.opPattern","COPY",BODY,{"derivedFrom":makeQuery(id+"F2.opPattern","COPY",BODY,{"derivedFrom":makeQuery(id+"F1.opRevolve","SWEPT_BODY",BODY,{"disambiguationData":[OSD([sQuery(id+"F0.wireOp",EDGE,"E1")])]}),"instanceName":"1"}),"instanceName":"1"}),"instanceName":"1"}),"instanceName":"1"}),"instanceName":"1"}),"instanceName":"1"}),"instanceName":"1"}),"instanceName":"1"});
            var Q2096;
            Q2096=makeQuery(id+"F13.opPattern","COPY",BODY,{"derivedFrom":makeQuery(id+"F11.opPattern","COPY",BODY,{"derivedFrom":makeQuery(id+"F9.opPattern","COPY",BODY,{"derivedFrom":makeQuery(id+"F8.opPattern","COPY",BODY,{"derivedFrom":makeQuery(id+"F7.opPattern","COPY",BODY,{"derivedFrom":makeQuery(id+"F5.opPattern","COPY",BODY,{"derivedFrom":makeQuery(id+"F4.opPattern","COPY",BODY,{"derivedFrom":makeQuery(id+"F1.opRevolve","SWEPT_BODY",BODY,{"disambiguationData":[OSD([sQuery(id+"F0.wireOp",EDGE,"E1")])]}),"instanceName":"1"}),"instanceName":"1"}),"instanceName":"1"}),"instanceName":"1"}),"instanceName":"1"}),"instanceName":"1"}),"instanceName":"1"});
            var Q2097;
            Q2097=makeQuery(id+"F13.opPattern","COPY",BODY,{"derivedFrom":makeQuery(id+"F11.opPattern","COPY",BODY,{"derivedFrom":makeQuery(id+"F9.opPattern","COPY",BODY,{"derivedFrom":makeQuery(id+"F8.opPattern","COPY",BODY,{"derivedFrom":makeQuery(id+"F7.opPattern","COPY",BODY,{"derivedFrom":makeQuery(id+"F5.opPattern","COPY",BODY,{"derivedFrom":makeQuery(id+"F4.opPattern","COPY",BODY,{"derivedFrom":makeQuery(id+"F2.opPattern","COPY",BODY,{"derivedFrom":makeQuery(id+"F1.opRevolve","SWEPT_BODY",BODY,{"disambiguationData":[OSD([sQuery(id+"F0.wireOp",EDGE,"E1")])]}),"instanceName":"1"}),"instanceName":"1"}),"instanceName":"1"}),"instanceName":"1"}),"instanceName":"1"}),"instanceName":"1"}),"instanceName":"1"}),"instanceName":"1"});
            var Q2098;
            Q2098=makeQuery(id+"F13.opPattern","COPY",BODY,{"derivedFrom":makeQuery(id+"F11.opPattern","COPY",BODY,{"derivedFrom":makeQuery(id+"F9.opPattern","COPY",BODY,{"derivedFrom":makeQuery(id+"F8.opPattern","COPY",BODY,{"derivedFrom":makeQuery(id+"F7.opPattern","COPY",BODY,{"derivedFrom":makeQuery(id+"F5.opPattern","COPY",BODY,{"derivedFrom":makeQuery(id+"F4.opPattern","COPY",BODY,{"derivedFrom":makeQuery(id+"F3.opPattern","COPY",BODY,{"derivedFrom":makeQuery(id+"F2.opPattern","COPY",BODY,{"derivedFrom":makeQuery(id+"F1.opRevolve","SWEPT_BODY",BODY,{"disambiguationData":[OSD([sQuery(id+"F0.wireOp",EDGE,"E1")])]}),"instanceName":"1"}),"instanceName":"1"}),"instanceName":"1"}),"instanceName":"1"}),"instanceName":"1"}),"instanceName":"1"}),"instanceName":"1"}),"instanceName":"1"}),"instanceName":"1"});
            var Q2099;
            Q2099=makeQuery(id+"F13.opPattern","COPY",BODY,{"derivedFrom":makeQuery(id+"F11.opPattern","COPY",BODY,{"derivedFrom":makeQuery(id+"F9.opPattern","COPY",BODY,{"derivedFrom":makeQuery(id+"F8.opPattern","COPY",BODY,{"derivedFrom":makeQuery(id+"F7.opPattern","COPY",BODY,{"derivedFrom":makeQuery(id+"F6.opPattern","COPY",BODY,{"derivedFrom":makeQuery(id+"F1.opRevolve","SWEPT_BODY",BODY,{"disambiguationData":[OSD([sQuery(id+"F0.wireOp",EDGE,"E1")])]}),"instanceName":"1"}),"instanceName":"1"}),"instanceName":"1"}),"instanceName":"1"}),"instanceName":"1"}),"instanceName":"1"});
            var Q2100;
            Q2100=makeQuery(id+"F13.opPattern","COPY",BODY,{"derivedFrom":makeQuery(id+"F11.opPattern","COPY",BODY,{"derivedFrom":makeQuery(id+"F9.opPattern","COPY",BODY,{"derivedFrom":makeQuery(id+"F8.opPattern","COPY",BODY,{"derivedFrom":makeQuery(id+"F7.opPattern","COPY",BODY,{"derivedFrom":makeQuery(id+"F6.opPattern","COPY",BODY,{"derivedFrom":makeQuery(id+"F2.opPattern","COPY",BODY,{"derivedFrom":makeQuery(id+"F1.opRevolve","SWEPT_BODY",BODY,{"disambiguationData":[OSD([sQuery(id+"F0.wireOp",EDGE,"E1")])]}),"instanceName":"1"}),"instanceName":"1"}),"instanceName":"1"}),"instanceName":"1"}),"instanceName":"1"}),"instanceName":"1"}),"instanceName":"1"});
            var Q2101;
            Q2101=makeQuery(id+"F13.opPattern","COPY",BODY,{"derivedFrom":makeQuery(id+"F11.opPattern","COPY",BODY,{"derivedFrom":makeQuery(id+"F9.opPattern","COPY",BODY,{"derivedFrom":makeQuery(id+"F8.opPattern","COPY",BODY,{"derivedFrom":makeQuery(id+"F7.opPattern","COPY",BODY,{"derivedFrom":makeQuery(id+"F6.opPattern","COPY",BODY,{"derivedFrom":makeQuery(id+"F3.opPattern","COPY",BODY,{"derivedFrom":makeQuery(id+"F2.opPattern","COPY",BODY,{"derivedFrom":makeQuery(id+"F1.opRevolve","SWEPT_BODY",BODY,{"disambiguationData":[OSD([sQuery(id+"F0.wireOp",EDGE,"E1")])]}),"instanceName":"1"}),"instanceName":"1"}),"instanceName":"1"}),"instanceName":"1"}),"instanceName":"1"}),"instanceName":"1"}),"instanceName":"1"}),"instanceName":"1"});
            var Q2102;
            Q2102=makeQuery(id+"F13.opPattern","COPY",BODY,{"derivedFrom":makeQuery(id+"F11.opPattern","COPY",BODY,{"derivedFrom":makeQuery(id+"F9.opPattern","COPY",BODY,{"derivedFrom":makeQuery(id+"F8.opPattern","COPY",BODY,{"derivedFrom":makeQuery(id+"F7.opPattern","COPY",BODY,{"derivedFrom":makeQuery(id+"F6.opPattern","COPY",BODY,{"derivedFrom":makeQuery(id+"F4.opPattern","COPY",BODY,{"derivedFrom":makeQuery(id+"F1.opRevolve","SWEPT_BODY",BODY,{"disambiguationData":[OSD([sQuery(id+"F0.wireOp",EDGE,"E1")])]}),"instanceName":"1"}),"instanceName":"1"}),"instanceName":"1"}),"instanceName":"1"}),"instanceName":"1"}),"instanceName":"1"}),"instanceName":"1"});
            var Q2103;
            Q2103=makeQuery(id+"F13.opPattern","COPY",BODY,{"derivedFrom":makeQuery(id+"F11.opPattern","COPY",BODY,{"derivedFrom":makeQuery(id+"F9.opPattern","COPY",BODY,{"derivedFrom":makeQuery(id+"F8.opPattern","COPY",BODY,{"derivedFrom":makeQuery(id+"F7.opPattern","COPY",BODY,{"derivedFrom":makeQuery(id+"F6.opPattern","COPY",BODY,{"derivedFrom":makeQuery(id+"F4.opPattern","COPY",BODY,{"derivedFrom":makeQuery(id+"F2.opPattern","COPY",BODY,{"derivedFrom":makeQuery(id+"F1.opRevolve","SWEPT_BODY",BODY,{"disambiguationData":[OSD([sQuery(id+"F0.wireOp",EDGE,"E1")])]}),"instanceName":"1"}),"instanceName":"1"}),"instanceName":"1"}),"instanceName":"1"}),"instanceName":"1"}),"instanceName":"1"}),"instanceName":"1"}),"instanceName":"1"});
            var Q2104;
            Q2104=makeQuery(id+"F13.opPattern","COPY",BODY,{"derivedFrom":makeQuery(id+"F11.opPattern","COPY",BODY,{"derivedFrom":makeQuery(id+"F9.opPattern","COPY",BODY,{"derivedFrom":makeQuery(id+"F8.opPattern","COPY",BODY,{"derivedFrom":makeQuery(id+"F7.opPattern","COPY",BODY,{"derivedFrom":makeQuery(id+"F6.opPattern","COPY",BODY,{"derivedFrom":makeQuery(id+"F4.opPattern","COPY",BODY,{"derivedFrom":makeQuery(id+"F3.opPattern","COPY",BODY,{"derivedFrom":makeQuery(id+"F2.opPattern","COPY",BODY,{"derivedFrom":makeQuery(id+"F1.opRevolve","SWEPT_BODY",BODY,{"disambiguationData":[OSD([sQuery(id+"F0.wireOp",EDGE,"E1")])]}),"instanceName":"1"}),"instanceName":"1"}),"instanceName":"1"}),"instanceName":"1"}),"instanceName":"1"}),"instanceName":"1"}),"instanceName":"1"}),"instanceName":"1"}),"instanceName":"1"});
            var Q2105;
            Q2105=makeQuery(id+"F13.opPattern","COPY",BODY,{"derivedFrom":makeQuery(id+"F11.opPattern","COPY",BODY,{"derivedFrom":makeQuery(id+"F9.opPattern","COPY",BODY,{"derivedFrom":makeQuery(id+"F8.opPattern","COPY",BODY,{"derivedFrom":makeQuery(id+"F7.opPattern","COPY",BODY,{"derivedFrom":makeQuery(id+"F6.opPattern","COPY",BODY,{"derivedFrom":makeQuery(id+"F5.opPattern","COPY",BODY,{"derivedFrom":makeQuery(id+"F1.opRevolve","SWEPT_BODY",BODY,{"disambiguationData":[OSD([sQuery(id+"F0.wireOp",EDGE,"E1")])]}),"instanceName":"1"}),"instanceName":"1"}),"instanceName":"1"}),"instanceName":"1"}),"instanceName":"1"}),"instanceName":"1"}),"instanceName":"1"});
            var Q2106;
            Q2106=makeQuery(id+"F13.opPattern","COPY",BODY,{"derivedFrom":makeQuery(id+"F11.opPattern","COPY",BODY,{"derivedFrom":makeQuery(id+"F9.opPattern","COPY",BODY,{"derivedFrom":makeQuery(id+"F8.opPattern","COPY",BODY,{"derivedFrom":makeQuery(id+"F7.opPattern","COPY",BODY,{"derivedFrom":makeQuery(id+"F6.opPattern","COPY",BODY,{"derivedFrom":makeQuery(id+"F5.opPattern","COPY",BODY,{"derivedFrom":makeQuery(id+"F2.opPattern","COPY",BODY,{"derivedFrom":makeQuery(id+"F1.opRevolve","SWEPT_BODY",BODY,{"disambiguationData":[OSD([sQuery(id+"F0.wireOp",EDGE,"E1")])]}),"instanceName":"1"}),"instanceName":"1"}),"instanceName":"1"}),"instanceName":"1"}),"instanceName":"1"}),"instanceName":"1"}),"instanceName":"1"}),"instanceName":"1"});
            var Q2107;
            Q2107=makeQuery(id+"F13.opPattern","COPY",BODY,{"derivedFrom":makeQuery(id+"F11.opPattern","COPY",BODY,{"derivedFrom":makeQuery(id+"F9.opPattern","COPY",BODY,{"derivedFrom":makeQuery(id+"F8.opPattern","COPY",BODY,{"derivedFrom":makeQuery(id+"F7.opPattern","COPY",BODY,{"derivedFrom":makeQuery(id+"F6.opPattern","COPY",BODY,{"derivedFrom":makeQuery(id+"F5.opPattern","COPY",BODY,{"derivedFrom":makeQuery(id+"F3.opPattern","COPY",BODY,{"derivedFrom":makeQuery(id+"F2.opPattern","COPY",BODY,{"derivedFrom":makeQuery(id+"F1.opRevolve","SWEPT_BODY",BODY,{"disambiguationData":[OSD([sQuery(id+"F0.wireOp",EDGE,"E1")])]}),"instanceName":"1"}),"instanceName":"1"}),"instanceName":"1"}),"instanceName":"1"}),"instanceName":"1"}),"instanceName":"1"}),"instanceName":"1"}),"instanceName":"1"}),"instanceName":"1"});
            var Q2108;
            Q2108=makeQuery(id+"F13.opPattern","COPY",BODY,{"derivedFrom":makeQuery(id+"F11.opPattern","COPY",BODY,{"derivedFrom":makeQuery(id+"F9.opPattern","COPY",BODY,{"derivedFrom":makeQuery(id+"F8.opPattern","COPY",BODY,{"derivedFrom":makeQuery(id+"F7.opPattern","COPY",BODY,{"derivedFrom":makeQuery(id+"F6.opPattern","COPY",BODY,{"derivedFrom":makeQuery(id+"F5.opPattern","COPY",BODY,{"derivedFrom":makeQuery(id+"F4.opPattern","COPY",BODY,{"derivedFrom":makeQuery(id+"F1.opRevolve","SWEPT_BODY",BODY,{"disambiguationData":[OSD([sQuery(id+"F0.wireOp",EDGE,"E1")])]}),"instanceName":"1"}),"instanceName":"1"}),"instanceName":"1"}),"instanceName":"1"}),"instanceName":"1"}),"instanceName":"1"}),"instanceName":"1"}),"instanceName":"1"});
            var Q2109;
            Q2109=makeQuery(id+"F13.opPattern","COPY",BODY,{"derivedFrom":makeQuery(id+"F11.opPattern","COPY",BODY,{"derivedFrom":makeQuery(id+"F9.opPattern","COPY",BODY,{"derivedFrom":makeQuery(id+"F8.opPattern","COPY",BODY,{"derivedFrom":makeQuery(id+"F7.opPattern","COPY",BODY,{"derivedFrom":makeQuery(id+"F6.opPattern","COPY",BODY,{"derivedFrom":makeQuery(id+"F5.opPattern","COPY",BODY,{"derivedFrom":makeQuery(id+"F4.opPattern","COPY",BODY,{"derivedFrom":makeQuery(id+"F2.opPattern","COPY",BODY,{"derivedFrom":makeQuery(id+"F1.opRevolve","SWEPT_BODY",BODY,{"disambiguationData":[OSD([sQuery(id+"F0.wireOp",EDGE,"E1")])]}),"instanceName":"1"}),"instanceName":"1"}),"instanceName":"1"}),"instanceName":"1"}),"instanceName":"1"}),"instanceName":"1"}),"instanceName":"1"}),"instanceName":"1"}),"instanceName":"1"});
            var Q2110;
            Q2110=makeQuery(id+"F13.opPattern","COPY",BODY,{"derivedFrom":makeQuery(id+"F11.opPattern","COPY",BODY,{"derivedFrom":makeQuery(id+"F9.opPattern","COPY",BODY,{"derivedFrom":makeQuery(id+"F8.opPattern","COPY",BODY,{"derivedFrom":makeQuery(id+"F7.opPattern","COPY",BODY,{"derivedFrom":makeQuery(id+"F6.opPattern","COPY",BODY,{"derivedFrom":makeQuery(id+"F5.opPattern","COPY",BODY,{"derivedFrom":makeQuery(id+"F4.opPattern","COPY",BODY,{"derivedFrom":makeQuery(id+"F3.opPattern","COPY",BODY,{"derivedFrom":makeQuery(id+"F2.opPattern","COPY",BODY,{"derivedFrom":makeQuery(id+"F1.opRevolve","SWEPT_BODY",BODY,{"disambiguationData":[OSD([sQuery(id+"F0.wireOp",EDGE,"E1")])]}),"instanceName":"1"}),"instanceName":"1"}),"instanceName":"1"}),"instanceName":"1"}),"instanceName":"1"}),"instanceName":"1"}),"instanceName":"1"}),"instanceName":"1"}),"instanceName":"1"}),"instanceName":"1"});
            var Q2111;
            Q2111=makeQuery(id+"F13.opPattern","COPY",BODY,{"derivedFrom":makeQuery(id+"F11.opPattern","COPY",BODY,{"derivedFrom":makeQuery(id+"F10.opPattern","COPY",BODY,{"derivedFrom":makeQuery(id+"F1.opRevolve","SWEPT_BODY",BODY,{"disambiguationData":[OSD([sQuery(id+"F0.wireOp",EDGE,"E1")])]}),"instanceName":"1"}),"instanceName":"1"}),"instanceName":"1"});
            var Q2112;
            Q2112=makeQuery(id+"F13.opPattern","COPY",BODY,{"derivedFrom":makeQuery(id+"F11.opPattern","COPY",BODY,{"derivedFrom":makeQuery(id+"F10.opPattern","COPY",BODY,{"derivedFrom":makeQuery(id+"F2.opPattern","COPY",BODY,{"derivedFrom":makeQuery(id+"F1.opRevolve","SWEPT_BODY",BODY,{"disambiguationData":[OSD([sQuery(id+"F0.wireOp",EDGE,"E1")])]}),"instanceName":"1"}),"instanceName":"1"}),"instanceName":"1"}),"instanceName":"1"});
            var Q2113;
            Q2113=makeQuery(id+"F13.opPattern","COPY",BODY,{"derivedFrom":makeQuery(id+"F11.opPattern","COPY",BODY,{"derivedFrom":makeQuery(id+"F10.opPattern","COPY",BODY,{"derivedFrom":makeQuery(id+"F3.opPattern","COPY",BODY,{"derivedFrom":makeQuery(id+"F2.opPattern","COPY",BODY,{"derivedFrom":makeQuery(id+"F1.opRevolve","SWEPT_BODY",BODY,{"disambiguationData":[OSD([sQuery(id+"F0.wireOp",EDGE,"E1")])]}),"instanceName":"1"}),"instanceName":"1"}),"instanceName":"1"}),"instanceName":"1"}),"instanceName":"1"});
            var Q2114;
            Q2114=makeQuery(id+"F13.opPattern","COPY",BODY,{"derivedFrom":makeQuery(id+"F11.opPattern","COPY",BODY,{"derivedFrom":makeQuery(id+"F10.opPattern","COPY",BODY,{"derivedFrom":makeQuery(id+"F4.opPattern","COPY",BODY,{"derivedFrom":makeQuery(id+"F1.opRevolve","SWEPT_BODY",BODY,{"disambiguationData":[OSD([sQuery(id+"F0.wireOp",EDGE,"E1")])]}),"instanceName":"1"}),"instanceName":"1"}),"instanceName":"1"}),"instanceName":"1"});
            var Q2115;
            Q2115=makeQuery(id+"F13.opPattern","COPY",BODY,{"derivedFrom":makeQuery(id+"F11.opPattern","COPY",BODY,{"derivedFrom":makeQuery(id+"F10.opPattern","COPY",BODY,{"derivedFrom":makeQuery(id+"F4.opPattern","COPY",BODY,{"derivedFrom":makeQuery(id+"F2.opPattern","COPY",BODY,{"derivedFrom":makeQuery(id+"F1.opRevolve","SWEPT_BODY",BODY,{"disambiguationData":[OSD([sQuery(id+"F0.wireOp",EDGE,"E1")])]}),"instanceName":"1"}),"instanceName":"1"}),"instanceName":"1"}),"instanceName":"1"}),"instanceName":"1"});
            var Q2116;
            Q2116=makeQuery(id+"F13.opPattern","COPY",BODY,{"derivedFrom":makeQuery(id+"F11.opPattern","COPY",BODY,{"derivedFrom":makeQuery(id+"F10.opPattern","COPY",BODY,{"derivedFrom":makeQuery(id+"F4.opPattern","COPY",BODY,{"derivedFrom":makeQuery(id+"F3.opPattern","COPY",BODY,{"derivedFrom":makeQuery(id+"F2.opPattern","COPY",BODY,{"derivedFrom":makeQuery(id+"F1.opRevolve","SWEPT_BODY",BODY,{"disambiguationData":[OSD([sQuery(id+"F0.wireOp",EDGE,"E1")])]}),"instanceName":"1"}),"instanceName":"1"}),"instanceName":"1"}),"instanceName":"1"}),"instanceName":"1"}),"instanceName":"1"});
            var Q2117;
            Q2117=makeQuery(id+"F13.opPattern","COPY",BODY,{"derivedFrom":makeQuery(id+"F11.opPattern","COPY",BODY,{"derivedFrom":makeQuery(id+"F10.opPattern","COPY",BODY,{"derivedFrom":makeQuery(id+"F5.opPattern","COPY",BODY,{"derivedFrom":makeQuery(id+"F1.opRevolve","SWEPT_BODY",BODY,{"disambiguationData":[OSD([sQuery(id+"F0.wireOp",EDGE,"E1")])]}),"instanceName":"1"}),"instanceName":"1"}),"instanceName":"1"}),"instanceName":"1"});
            var Q2118;
            Q2118=makeQuery(id+"F13.opPattern","COPY",BODY,{"derivedFrom":makeQuery(id+"F11.opPattern","COPY",BODY,{"derivedFrom":makeQuery(id+"F10.opPattern","COPY",BODY,{"derivedFrom":makeQuery(id+"F5.opPattern","COPY",BODY,{"derivedFrom":makeQuery(id+"F2.opPattern","COPY",BODY,{"derivedFrom":makeQuery(id+"F1.opRevolve","SWEPT_BODY",BODY,{"disambiguationData":[OSD([sQuery(id+"F0.wireOp",EDGE,"E1")])]}),"instanceName":"1"}),"instanceName":"1"}),"instanceName":"1"}),"instanceName":"1"}),"instanceName":"1"});
            var Q2119;
            Q2119=makeQuery(id+"F13.opPattern","COPY",BODY,{"derivedFrom":makeQuery(id+"F11.opPattern","COPY",BODY,{"derivedFrom":makeQuery(id+"F10.opPattern","COPY",BODY,{"derivedFrom":makeQuery(id+"F5.opPattern","COPY",BODY,{"derivedFrom":makeQuery(id+"F3.opPattern","COPY",BODY,{"derivedFrom":makeQuery(id+"F2.opPattern","COPY",BODY,{"derivedFrom":makeQuery(id+"F1.opRevolve","SWEPT_BODY",BODY,{"disambiguationData":[OSD([sQuery(id+"F0.wireOp",EDGE,"E1")])]}),"instanceName":"1"}),"instanceName":"1"}),"instanceName":"1"}),"instanceName":"1"}),"instanceName":"1"}),"instanceName":"1"});
            var Q2120;
            Q2120=makeQuery(id+"F13.opPattern","COPY",BODY,{"derivedFrom":makeQuery(id+"F11.opPattern","COPY",BODY,{"derivedFrom":makeQuery(id+"F10.opPattern","COPY",BODY,{"derivedFrom":makeQuery(id+"F5.opPattern","COPY",BODY,{"derivedFrom":makeQuery(id+"F4.opPattern","COPY",BODY,{"derivedFrom":makeQuery(id+"F1.opRevolve","SWEPT_BODY",BODY,{"disambiguationData":[OSD([sQuery(id+"F0.wireOp",EDGE,"E1")])]}),"instanceName":"1"}),"instanceName":"1"}),"instanceName":"1"}),"instanceName":"1"}),"instanceName":"1"});
            var Q2121;
            Q2121=makeQuery(id+"F13.opPattern","COPY",BODY,{"derivedFrom":makeQuery(id+"F11.opPattern","COPY",BODY,{"derivedFrom":makeQuery(id+"F10.opPattern","COPY",BODY,{"derivedFrom":makeQuery(id+"F5.opPattern","COPY",BODY,{"derivedFrom":makeQuery(id+"F4.opPattern","COPY",BODY,{"derivedFrom":makeQuery(id+"F2.opPattern","COPY",BODY,{"derivedFrom":makeQuery(id+"F1.opRevolve","SWEPT_BODY",BODY,{"disambiguationData":[OSD([sQuery(id+"F0.wireOp",EDGE,"E1")])]}),"instanceName":"1"}),"instanceName":"1"}),"instanceName":"1"}),"instanceName":"1"}),"instanceName":"1"}),"instanceName":"1"});
            var Q2122;
            Q2122=makeQuery(id+"F13.opPattern","COPY",BODY,{"derivedFrom":makeQuery(id+"F11.opPattern","COPY",BODY,{"derivedFrom":makeQuery(id+"F10.opPattern","COPY",BODY,{"derivedFrom":makeQuery(id+"F5.opPattern","COPY",BODY,{"derivedFrom":makeQuery(id+"F4.opPattern","COPY",BODY,{"derivedFrom":makeQuery(id+"F3.opPattern","COPY",BODY,{"derivedFrom":makeQuery(id+"F2.opPattern","COPY",BODY,{"derivedFrom":makeQuery(id+"F1.opRevolve","SWEPT_BODY",BODY,{"disambiguationData":[OSD([sQuery(id+"F0.wireOp",EDGE,"E1")])]}),"instanceName":"1"}),"instanceName":"1"}),"instanceName":"1"}),"instanceName":"1"}),"instanceName":"1"}),"instanceName":"1"}),"instanceName":"1"});
            var Q2123;
            Q2123=makeQuery(id+"F13.opPattern","COPY",BODY,{"derivedFrom":makeQuery(id+"F11.opPattern","COPY",BODY,{"derivedFrom":makeQuery(id+"F10.opPattern","COPY",BODY,{"derivedFrom":makeQuery(id+"F6.opPattern","COPY",BODY,{"derivedFrom":makeQuery(id+"F1.opRevolve","SWEPT_BODY",BODY,{"disambiguationData":[OSD([sQuery(id+"F0.wireOp",EDGE,"E1")])]}),"instanceName":"1"}),"instanceName":"1"}),"instanceName":"1"}),"instanceName":"1"});
            var Q2124;
            Q2124=makeQuery(id+"F13.opPattern","COPY",BODY,{"derivedFrom":makeQuery(id+"F11.opPattern","COPY",BODY,{"derivedFrom":makeQuery(id+"F10.opPattern","COPY",BODY,{"derivedFrom":makeQuery(id+"F6.opPattern","COPY",BODY,{"derivedFrom":makeQuery(id+"F2.opPattern","COPY",BODY,{"derivedFrom":makeQuery(id+"F1.opRevolve","SWEPT_BODY",BODY,{"disambiguationData":[OSD([sQuery(id+"F0.wireOp",EDGE,"E1")])]}),"instanceName":"1"}),"instanceName":"1"}),"instanceName":"1"}),"instanceName":"1"}),"instanceName":"1"});
            var Q2125;
            Q2125=makeQuery(id+"F13.opPattern","COPY",BODY,{"derivedFrom":makeQuery(id+"F11.opPattern","COPY",BODY,{"derivedFrom":makeQuery(id+"F10.opPattern","COPY",BODY,{"derivedFrom":makeQuery(id+"F6.opPattern","COPY",BODY,{"derivedFrom":makeQuery(id+"F3.opPattern","COPY",BODY,{"derivedFrom":makeQuery(id+"F2.opPattern","COPY",BODY,{"derivedFrom":makeQuery(id+"F1.opRevolve","SWEPT_BODY",BODY,{"disambiguationData":[OSD([sQuery(id+"F0.wireOp",EDGE,"E1")])]}),"instanceName":"1"}),"instanceName":"1"}),"instanceName":"1"}),"instanceName":"1"}),"instanceName":"1"}),"instanceName":"1"});
            var Q2126;
            Q2126=makeQuery(id+"F13.opPattern","COPY",BODY,{"derivedFrom":makeQuery(id+"F11.opPattern","COPY",BODY,{"derivedFrom":makeQuery(id+"F10.opPattern","COPY",BODY,{"derivedFrom":makeQuery(id+"F6.opPattern","COPY",BODY,{"derivedFrom":makeQuery(id+"F4.opPattern","COPY",BODY,{"derivedFrom":makeQuery(id+"F1.opRevolve","SWEPT_BODY",BODY,{"disambiguationData":[OSD([sQuery(id+"F0.wireOp",EDGE,"E1")])]}),"instanceName":"1"}),"instanceName":"1"}),"instanceName":"1"}),"instanceName":"1"}),"instanceName":"1"});
            var Q2127;
            Q2127=makeQuery(id+"F13.opPattern","COPY",BODY,{"derivedFrom":makeQuery(id+"F11.opPattern","COPY",BODY,{"derivedFrom":makeQuery(id+"F10.opPattern","COPY",BODY,{"derivedFrom":makeQuery(id+"F6.opPattern","COPY",BODY,{"derivedFrom":makeQuery(id+"F4.opPattern","COPY",BODY,{"derivedFrom":makeQuery(id+"F2.opPattern","COPY",BODY,{"derivedFrom":makeQuery(id+"F1.opRevolve","SWEPT_BODY",BODY,{"disambiguationData":[OSD([sQuery(id+"F0.wireOp",EDGE,"E1")])]}),"instanceName":"1"}),"instanceName":"1"}),"instanceName":"1"}),"instanceName":"1"}),"instanceName":"1"}),"instanceName":"1"});
            var Q2128;
            Q2128=makeQuery(id+"F13.opPattern","COPY",BODY,{"derivedFrom":makeQuery(id+"F11.opPattern","COPY",BODY,{"derivedFrom":makeQuery(id+"F10.opPattern","COPY",BODY,{"derivedFrom":makeQuery(id+"F6.opPattern","COPY",BODY,{"derivedFrom":makeQuery(id+"F4.opPattern","COPY",BODY,{"derivedFrom":makeQuery(id+"F3.opPattern","COPY",BODY,{"derivedFrom":makeQuery(id+"F2.opPattern","COPY",BODY,{"derivedFrom":makeQuery(id+"F1.opRevolve","SWEPT_BODY",BODY,{"disambiguationData":[OSD([sQuery(id+"F0.wireOp",EDGE,"E1")])]}),"instanceName":"1"}),"instanceName":"1"}),"instanceName":"1"}),"instanceName":"1"}),"instanceName":"1"}),"instanceName":"1"}),"instanceName":"1"});
            var Q2129;
            Q2129=makeQuery(id+"F13.opPattern","COPY",BODY,{"derivedFrom":makeQuery(id+"F11.opPattern","COPY",BODY,{"derivedFrom":makeQuery(id+"F10.opPattern","COPY",BODY,{"derivedFrom":makeQuery(id+"F6.opPattern","COPY",BODY,{"derivedFrom":makeQuery(id+"F5.opPattern","COPY",BODY,{"derivedFrom":makeQuery(id+"F1.opRevolve","SWEPT_BODY",BODY,{"disambiguationData":[OSD([sQuery(id+"F0.wireOp",EDGE,"E1")])]}),"instanceName":"1"}),"instanceName":"1"}),"instanceName":"1"}),"instanceName":"1"}),"instanceName":"1"});
            var Q2130;
            Q2130=makeQuery(id+"F13.opPattern","COPY",BODY,{"derivedFrom":makeQuery(id+"F11.opPattern","COPY",BODY,{"derivedFrom":makeQuery(id+"F10.opPattern","COPY",BODY,{"derivedFrom":makeQuery(id+"F6.opPattern","COPY",BODY,{"derivedFrom":makeQuery(id+"F5.opPattern","COPY",BODY,{"derivedFrom":makeQuery(id+"F2.opPattern","COPY",BODY,{"derivedFrom":makeQuery(id+"F1.opRevolve","SWEPT_BODY",BODY,{"disambiguationData":[OSD([sQuery(id+"F0.wireOp",EDGE,"E1")])]}),"instanceName":"1"}),"instanceName":"1"}),"instanceName":"1"}),"instanceName":"1"}),"instanceName":"1"}),"instanceName":"1"});
            var Q2131;
            Q2131=makeQuery(id+"F13.opPattern","COPY",BODY,{"derivedFrom":makeQuery(id+"F11.opPattern","COPY",BODY,{"derivedFrom":makeQuery(id+"F10.opPattern","COPY",BODY,{"derivedFrom":makeQuery(id+"F6.opPattern","COPY",BODY,{"derivedFrom":makeQuery(id+"F5.opPattern","COPY",BODY,{"derivedFrom":makeQuery(id+"F3.opPattern","COPY",BODY,{"derivedFrom":makeQuery(id+"F2.opPattern","COPY",BODY,{"derivedFrom":makeQuery(id+"F1.opRevolve","SWEPT_BODY",BODY,{"disambiguationData":[OSD([sQuery(id+"F0.wireOp",EDGE,"E1")])]}),"instanceName":"1"}),"instanceName":"1"}),"instanceName":"1"}),"instanceName":"1"}),"instanceName":"1"}),"instanceName":"1"}),"instanceName":"1"});
            var Q2132;
            Q2132=makeQuery(id+"F13.opPattern","COPY",BODY,{"derivedFrom":makeQuery(id+"F11.opPattern","COPY",BODY,{"derivedFrom":makeQuery(id+"F10.opPattern","COPY",BODY,{"derivedFrom":makeQuery(id+"F6.opPattern","COPY",BODY,{"derivedFrom":makeQuery(id+"F5.opPattern","COPY",BODY,{"derivedFrom":makeQuery(id+"F4.opPattern","COPY",BODY,{"derivedFrom":makeQuery(id+"F1.opRevolve","SWEPT_BODY",BODY,{"disambiguationData":[OSD([sQuery(id+"F0.wireOp",EDGE,"E1")])]}),"instanceName":"1"}),"instanceName":"1"}),"instanceName":"1"}),"instanceName":"1"}),"instanceName":"1"}),"instanceName":"1"});
            var Q2133;
            Q2133=makeQuery(id+"F13.opPattern","COPY",BODY,{"derivedFrom":makeQuery(id+"F11.opPattern","COPY",BODY,{"derivedFrom":makeQuery(id+"F10.opPattern","COPY",BODY,{"derivedFrom":makeQuery(id+"F6.opPattern","COPY",BODY,{"derivedFrom":makeQuery(id+"F5.opPattern","COPY",BODY,{"derivedFrom":makeQuery(id+"F4.opPattern","COPY",BODY,{"derivedFrom":makeQuery(id+"F2.opPattern","COPY",BODY,{"derivedFrom":makeQuery(id+"F1.opRevolve","SWEPT_BODY",BODY,{"disambiguationData":[OSD([sQuery(id+"F0.wireOp",EDGE,"E1")])]}),"instanceName":"1"}),"instanceName":"1"}),"instanceName":"1"}),"instanceName":"1"}),"instanceName":"1"}),"instanceName":"1"}),"instanceName":"1"});
            var Q2134;
            Q2134=makeQuery(id+"F13.opPattern","COPY",BODY,{"derivedFrom":makeQuery(id+"F11.opPattern","COPY",BODY,{"derivedFrom":makeQuery(id+"F10.opPattern","COPY",BODY,{"derivedFrom":makeQuery(id+"F6.opPattern","COPY",BODY,{"derivedFrom":makeQuery(id+"F5.opPattern","COPY",BODY,{"derivedFrom":makeQuery(id+"F4.opPattern","COPY",BODY,{"derivedFrom":makeQuery(id+"F3.opPattern","COPY",BODY,{"derivedFrom":makeQuery(id+"F2.opPattern","COPY",BODY,{"derivedFrom":makeQuery(id+"F1.opRevolve","SWEPT_BODY",BODY,{"disambiguationData":[OSD([sQuery(id+"F0.wireOp",EDGE,"E1")])]}),"instanceName":"1"}),"instanceName":"1"}),"instanceName":"1"}),"instanceName":"1"}),"instanceName":"1"}),"instanceName":"1"}),"instanceName":"1"}),"instanceName":"1"});
            var Q2135;
            Q2135=makeQuery(id+"F13.opPattern","COPY",BODY,{"derivedFrom":makeQuery(id+"F11.opPattern","COPY",BODY,{"derivedFrom":makeQuery(id+"F10.opPattern","COPY",BODY,{"derivedFrom":makeQuery(id+"F7.opPattern","COPY",BODY,{"derivedFrom":makeQuery(id+"F1.opRevolve","SWEPT_BODY",BODY,{"disambiguationData":[OSD([sQuery(id+"F0.wireOp",EDGE,"E1")])]}),"instanceName":"1"}),"instanceName":"1"}),"instanceName":"1"}),"instanceName":"1"});
            var Q2136;
            Q2136=makeQuery(id+"F13.opPattern","COPY",BODY,{"derivedFrom":makeQuery(id+"F11.opPattern","COPY",BODY,{"derivedFrom":makeQuery(id+"F10.opPattern","COPY",BODY,{"derivedFrom":makeQuery(id+"F7.opPattern","COPY",BODY,{"derivedFrom":makeQuery(id+"F2.opPattern","COPY",BODY,{"derivedFrom":makeQuery(id+"F1.opRevolve","SWEPT_BODY",BODY,{"disambiguationData":[OSD([sQuery(id+"F0.wireOp",EDGE,"E1")])]}),"instanceName":"1"}),"instanceName":"1"}),"instanceName":"1"}),"instanceName":"1"}),"instanceName":"1"});
            var Q2137;
            Q2137=makeQuery(id+"F13.opPattern","COPY",BODY,{"derivedFrom":makeQuery(id+"F11.opPattern","COPY",BODY,{"derivedFrom":makeQuery(id+"F10.opPattern","COPY",BODY,{"derivedFrom":makeQuery(id+"F7.opPattern","COPY",BODY,{"derivedFrom":makeQuery(id+"F3.opPattern","COPY",BODY,{"derivedFrom":makeQuery(id+"F2.opPattern","COPY",BODY,{"derivedFrom":makeQuery(id+"F1.opRevolve","SWEPT_BODY",BODY,{"disambiguationData":[OSD([sQuery(id+"F0.wireOp",EDGE,"E1")])]}),"instanceName":"1"}),"instanceName":"1"}),"instanceName":"1"}),"instanceName":"1"}),"instanceName":"1"}),"instanceName":"1"});
            var Q2138;
            Q2138=makeQuery(id+"F13.opPattern","COPY",BODY,{"derivedFrom":makeQuery(id+"F11.opPattern","COPY",BODY,{"derivedFrom":makeQuery(id+"F10.opPattern","COPY",BODY,{"derivedFrom":makeQuery(id+"F7.opPattern","COPY",BODY,{"derivedFrom":makeQuery(id+"F4.opPattern","COPY",BODY,{"derivedFrom":makeQuery(id+"F1.opRevolve","SWEPT_BODY",BODY,{"disambiguationData":[OSD([sQuery(id+"F0.wireOp",EDGE,"E1")])]}),"instanceName":"1"}),"instanceName":"1"}),"instanceName":"1"}),"instanceName":"1"}),"instanceName":"1"});
            var Q2139;
            Q2139=makeQuery(id+"F13.opPattern","COPY",BODY,{"derivedFrom":makeQuery(id+"F11.opPattern","COPY",BODY,{"derivedFrom":makeQuery(id+"F10.opPattern","COPY",BODY,{"derivedFrom":makeQuery(id+"F7.opPattern","COPY",BODY,{"derivedFrom":makeQuery(id+"F4.opPattern","COPY",BODY,{"derivedFrom":makeQuery(id+"F2.opPattern","COPY",BODY,{"derivedFrom":makeQuery(id+"F1.opRevolve","SWEPT_BODY",BODY,{"disambiguationData":[OSD([sQuery(id+"F0.wireOp",EDGE,"E1")])]}),"instanceName":"1"}),"instanceName":"1"}),"instanceName":"1"}),"instanceName":"1"}),"instanceName":"1"}),"instanceName":"1"});
            var Q2140;
            Q2140=makeQuery(id+"F13.opPattern","COPY",BODY,{"derivedFrom":makeQuery(id+"F11.opPattern","COPY",BODY,{"derivedFrom":makeQuery(id+"F10.opPattern","COPY",BODY,{"derivedFrom":makeQuery(id+"F7.opPattern","COPY",BODY,{"derivedFrom":makeQuery(id+"F4.opPattern","COPY",BODY,{"derivedFrom":makeQuery(id+"F3.opPattern","COPY",BODY,{"derivedFrom":makeQuery(id+"F2.opPattern","COPY",BODY,{"derivedFrom":makeQuery(id+"F1.opRevolve","SWEPT_BODY",BODY,{"disambiguationData":[OSD([sQuery(id+"F0.wireOp",EDGE,"E1")])]}),"instanceName":"1"}),"instanceName":"1"}),"instanceName":"1"}),"instanceName":"1"}),"instanceName":"1"}),"instanceName":"1"}),"instanceName":"1"});
            var Q2141;
            Q2141=makeQuery(id+"F13.opPattern","COPY",BODY,{"derivedFrom":makeQuery(id+"F11.opPattern","COPY",BODY,{"derivedFrom":makeQuery(id+"F10.opPattern","COPY",BODY,{"derivedFrom":makeQuery(id+"F7.opPattern","COPY",BODY,{"derivedFrom":makeQuery(id+"F5.opPattern","COPY",BODY,{"derivedFrom":makeQuery(id+"F1.opRevolve","SWEPT_BODY",BODY,{"disambiguationData":[OSD([sQuery(id+"F0.wireOp",EDGE,"E1")])]}),"instanceName":"1"}),"instanceName":"1"}),"instanceName":"1"}),"instanceName":"1"}),"instanceName":"1"});
            var Q2142;
            Q2142=makeQuery(id+"F13.opPattern","COPY",BODY,{"derivedFrom":makeQuery(id+"F11.opPattern","COPY",BODY,{"derivedFrom":makeQuery(id+"F10.opPattern","COPY",BODY,{"derivedFrom":makeQuery(id+"F7.opPattern","COPY",BODY,{"derivedFrom":makeQuery(id+"F5.opPattern","COPY",BODY,{"derivedFrom":makeQuery(id+"F2.opPattern","COPY",BODY,{"derivedFrom":makeQuery(id+"F1.opRevolve","SWEPT_BODY",BODY,{"disambiguationData":[OSD([sQuery(id+"F0.wireOp",EDGE,"E1")])]}),"instanceName":"1"}),"instanceName":"1"}),"instanceName":"1"}),"instanceName":"1"}),"instanceName":"1"}),"instanceName":"1"});
            var Q2143;
            Q2143=makeQuery(id+"F13.opPattern","COPY",BODY,{"derivedFrom":makeQuery(id+"F11.opPattern","COPY",BODY,{"derivedFrom":makeQuery(id+"F10.opPattern","COPY",BODY,{"derivedFrom":makeQuery(id+"F7.opPattern","COPY",BODY,{"derivedFrom":makeQuery(id+"F5.opPattern","COPY",BODY,{"derivedFrom":makeQuery(id+"F3.opPattern","COPY",BODY,{"derivedFrom":makeQuery(id+"F2.opPattern","COPY",BODY,{"derivedFrom":makeQuery(id+"F1.opRevolve","SWEPT_BODY",BODY,{"disambiguationData":[OSD([sQuery(id+"F0.wireOp",EDGE,"E1")])]}),"instanceName":"1"}),"instanceName":"1"}),"instanceName":"1"}),"instanceName":"1"}),"instanceName":"1"}),"instanceName":"1"}),"instanceName":"1"});
            var Q2144;
            Q2144=makeQuery(id+"F13.opPattern","COPY",BODY,{"derivedFrom":makeQuery(id+"F11.opPattern","COPY",BODY,{"derivedFrom":makeQuery(id+"F10.opPattern","COPY",BODY,{"derivedFrom":makeQuery(id+"F7.opPattern","COPY",BODY,{"derivedFrom":makeQuery(id+"F5.opPattern","COPY",BODY,{"derivedFrom":makeQuery(id+"F4.opPattern","COPY",BODY,{"derivedFrom":makeQuery(id+"F1.opRevolve","SWEPT_BODY",BODY,{"disambiguationData":[OSD([sQuery(id+"F0.wireOp",EDGE,"E1")])]}),"instanceName":"1"}),"instanceName":"1"}),"instanceName":"1"}),"instanceName":"1"}),"instanceName":"1"}),"instanceName":"1"});
            var Q2145;
            Q2145=makeQuery(id+"F13.opPattern","COPY",BODY,{"derivedFrom":makeQuery(id+"F11.opPattern","COPY",BODY,{"derivedFrom":makeQuery(id+"F10.opPattern","COPY",BODY,{"derivedFrom":makeQuery(id+"F7.opPattern","COPY",BODY,{"derivedFrom":makeQuery(id+"F5.opPattern","COPY",BODY,{"derivedFrom":makeQuery(id+"F4.opPattern","COPY",BODY,{"derivedFrom":makeQuery(id+"F2.opPattern","COPY",BODY,{"derivedFrom":makeQuery(id+"F1.opRevolve","SWEPT_BODY",BODY,{"disambiguationData":[OSD([sQuery(id+"F0.wireOp",EDGE,"E1")])]}),"instanceName":"1"}),"instanceName":"1"}),"instanceName":"1"}),"instanceName":"1"}),"instanceName":"1"}),"instanceName":"1"}),"instanceName":"1"});
            var Q2146;
            Q2146=makeQuery(id+"F13.opPattern","COPY",BODY,{"derivedFrom":makeQuery(id+"F11.opPattern","COPY",BODY,{"derivedFrom":makeQuery(id+"F10.opPattern","COPY",BODY,{"derivedFrom":makeQuery(id+"F7.opPattern","COPY",BODY,{"derivedFrom":makeQuery(id+"F5.opPattern","COPY",BODY,{"derivedFrom":makeQuery(id+"F4.opPattern","COPY",BODY,{"derivedFrom":makeQuery(id+"F3.opPattern","COPY",BODY,{"derivedFrom":makeQuery(id+"F2.opPattern","COPY",BODY,{"derivedFrom":makeQuery(id+"F1.opRevolve","SWEPT_BODY",BODY,{"disambiguationData":[OSD([sQuery(id+"F0.wireOp",EDGE,"E1")])]}),"instanceName":"1"}),"instanceName":"1"}),"instanceName":"1"}),"instanceName":"1"}),"instanceName":"1"}),"instanceName":"1"}),"instanceName":"1"}),"instanceName":"1"});
            var Q2147;
            Q2147=makeQuery(id+"F13.opPattern","COPY",BODY,{"derivedFrom":makeQuery(id+"F11.opPattern","COPY",BODY,{"derivedFrom":makeQuery(id+"F10.opPattern","COPY",BODY,{"derivedFrom":makeQuery(id+"F7.opPattern","COPY",BODY,{"derivedFrom":makeQuery(id+"F6.opPattern","COPY",BODY,{"derivedFrom":makeQuery(id+"F1.opRevolve","SWEPT_BODY",BODY,{"disambiguationData":[OSD([sQuery(id+"F0.wireOp",EDGE,"E1")])]}),"instanceName":"1"}),"instanceName":"1"}),"instanceName":"1"}),"instanceName":"1"}),"instanceName":"1"});
            var Q2148;
            Q2148=makeQuery(id+"F13.opPattern","COPY",BODY,{"derivedFrom":makeQuery(id+"F11.opPattern","COPY",BODY,{"derivedFrom":makeQuery(id+"F10.opPattern","COPY",BODY,{"derivedFrom":makeQuery(id+"F7.opPattern","COPY",BODY,{"derivedFrom":makeQuery(id+"F6.opPattern","COPY",BODY,{"derivedFrom":makeQuery(id+"F2.opPattern","COPY",BODY,{"derivedFrom":makeQuery(id+"F1.opRevolve","SWEPT_BODY",BODY,{"disambiguationData":[OSD([sQuery(id+"F0.wireOp",EDGE,"E1")])]}),"instanceName":"1"}),"instanceName":"1"}),"instanceName":"1"}),"instanceName":"1"}),"instanceName":"1"}),"instanceName":"1"});
            var Q2149;
            Q2149=makeQuery(id+"F13.opPattern","COPY",BODY,{"derivedFrom":makeQuery(id+"F11.opPattern","COPY",BODY,{"derivedFrom":makeQuery(id+"F10.opPattern","COPY",BODY,{"derivedFrom":makeQuery(id+"F7.opPattern","COPY",BODY,{"derivedFrom":makeQuery(id+"F6.opPattern","COPY",BODY,{"derivedFrom":makeQuery(id+"F3.opPattern","COPY",BODY,{"derivedFrom":makeQuery(id+"F2.opPattern","COPY",BODY,{"derivedFrom":makeQuery(id+"F1.opRevolve","SWEPT_BODY",BODY,{"disambiguationData":[OSD([sQuery(id+"F0.wireOp",EDGE,"E1")])]}),"instanceName":"1"}),"instanceName":"1"}),"instanceName":"1"}),"instanceName":"1"}),"instanceName":"1"}),"instanceName":"1"}),"instanceName":"1"});
            var Q2150;
            Q2150=makeQuery(id+"F13.opPattern","COPY",BODY,{"derivedFrom":makeQuery(id+"F11.opPattern","COPY",BODY,{"derivedFrom":makeQuery(id+"F10.opPattern","COPY",BODY,{"derivedFrom":makeQuery(id+"F7.opPattern","COPY",BODY,{"derivedFrom":makeQuery(id+"F6.opPattern","COPY",BODY,{"derivedFrom":makeQuery(id+"F4.opPattern","COPY",BODY,{"derivedFrom":makeQuery(id+"F1.opRevolve","SWEPT_BODY",BODY,{"disambiguationData":[OSD([sQuery(id+"F0.wireOp",EDGE,"E1")])]}),"instanceName":"1"}),"instanceName":"1"}),"instanceName":"1"}),"instanceName":"1"}),"instanceName":"1"}),"instanceName":"1"});
            var Q2151;
            Q2151=makeQuery(id+"F13.opPattern","COPY",BODY,{"derivedFrom":makeQuery(id+"F11.opPattern","COPY",BODY,{"derivedFrom":makeQuery(id+"F10.opPattern","COPY",BODY,{"derivedFrom":makeQuery(id+"F7.opPattern","COPY",BODY,{"derivedFrom":makeQuery(id+"F6.opPattern","COPY",BODY,{"derivedFrom":makeQuery(id+"F4.opPattern","COPY",BODY,{"derivedFrom":makeQuery(id+"F2.opPattern","COPY",BODY,{"derivedFrom":makeQuery(id+"F1.opRevolve","SWEPT_BODY",BODY,{"disambiguationData":[OSD([sQuery(id+"F0.wireOp",EDGE,"E1")])]}),"instanceName":"1"}),"instanceName":"1"}),"instanceName":"1"}),"instanceName":"1"}),"instanceName":"1"}),"instanceName":"1"}),"instanceName":"1"});
            var Q2152;
            Q2152=makeQuery(id+"F13.opPattern","COPY",BODY,{"derivedFrom":makeQuery(id+"F11.opPattern","COPY",BODY,{"derivedFrom":makeQuery(id+"F10.opPattern","COPY",BODY,{"derivedFrom":makeQuery(id+"F7.opPattern","COPY",BODY,{"derivedFrom":makeQuery(id+"F6.opPattern","COPY",BODY,{"derivedFrom":makeQuery(id+"F4.opPattern","COPY",BODY,{"derivedFrom":makeQuery(id+"F3.opPattern","COPY",BODY,{"derivedFrom":makeQuery(id+"F2.opPattern","COPY",BODY,{"derivedFrom":makeQuery(id+"F1.opRevolve","SWEPT_BODY",BODY,{"disambiguationData":[OSD([sQuery(id+"F0.wireOp",EDGE,"E1")])]}),"instanceName":"1"}),"instanceName":"1"}),"instanceName":"1"}),"instanceName":"1"}),"instanceName":"1"}),"instanceName":"1"}),"instanceName":"1"}),"instanceName":"1"});
            var Q2153;
            Q2153=makeQuery(id+"F13.opPattern","COPY",BODY,{"derivedFrom":makeQuery(id+"F11.opPattern","COPY",BODY,{"derivedFrom":makeQuery(id+"F10.opPattern","COPY",BODY,{"derivedFrom":makeQuery(id+"F7.opPattern","COPY",BODY,{"derivedFrom":makeQuery(id+"F6.opPattern","COPY",BODY,{"derivedFrom":makeQuery(id+"F5.opPattern","COPY",BODY,{"derivedFrom":makeQuery(id+"F1.opRevolve","SWEPT_BODY",BODY,{"disambiguationData":[OSD([sQuery(id+"F0.wireOp",EDGE,"E1")])]}),"instanceName":"1"}),"instanceName":"1"}),"instanceName":"1"}),"instanceName":"1"}),"instanceName":"1"}),"instanceName":"1"});
            var Q2154;
            Q2154=makeQuery(id+"F13.opPattern","COPY",BODY,{"derivedFrom":makeQuery(id+"F11.opPattern","COPY",BODY,{"derivedFrom":makeQuery(id+"F10.opPattern","COPY",BODY,{"derivedFrom":makeQuery(id+"F7.opPattern","COPY",BODY,{"derivedFrom":makeQuery(id+"F6.opPattern","COPY",BODY,{"derivedFrom":makeQuery(id+"F5.opPattern","COPY",BODY,{"derivedFrom":makeQuery(id+"F2.opPattern","COPY",BODY,{"derivedFrom":makeQuery(id+"F1.opRevolve","SWEPT_BODY",BODY,{"disambiguationData":[OSD([sQuery(id+"F0.wireOp",EDGE,"E1")])]}),"instanceName":"1"}),"instanceName":"1"}),"instanceName":"1"}),"instanceName":"1"}),"instanceName":"1"}),"instanceName":"1"}),"instanceName":"1"});
            var Q2155;
            Q2155=makeQuery(id+"F13.opPattern","COPY",BODY,{"derivedFrom":makeQuery(id+"F11.opPattern","COPY",BODY,{"derivedFrom":makeQuery(id+"F10.opPattern","COPY",BODY,{"derivedFrom":makeQuery(id+"F7.opPattern","COPY",BODY,{"derivedFrom":makeQuery(id+"F6.opPattern","COPY",BODY,{"derivedFrom":makeQuery(id+"F5.opPattern","COPY",BODY,{"derivedFrom":makeQuery(id+"F3.opPattern","COPY",BODY,{"derivedFrom":makeQuery(id+"F2.opPattern","COPY",BODY,{"derivedFrom":makeQuery(id+"F1.opRevolve","SWEPT_BODY",BODY,{"disambiguationData":[OSD([sQuery(id+"F0.wireOp",EDGE,"E1")])]}),"instanceName":"1"}),"instanceName":"1"}),"instanceName":"1"}),"instanceName":"1"}),"instanceName":"1"}),"instanceName":"1"}),"instanceName":"1"}),"instanceName":"1"});
            var Q2156;
            Q2156=makeQuery(id+"F13.opPattern","COPY",BODY,{"derivedFrom":makeQuery(id+"F11.opPattern","COPY",BODY,{"derivedFrom":makeQuery(id+"F10.opPattern","COPY",BODY,{"derivedFrom":makeQuery(id+"F7.opPattern","COPY",BODY,{"derivedFrom":makeQuery(id+"F6.opPattern","COPY",BODY,{"derivedFrom":makeQuery(id+"F5.opPattern","COPY",BODY,{"derivedFrom":makeQuery(id+"F4.opPattern","COPY",BODY,{"derivedFrom":makeQuery(id+"F1.opRevolve","SWEPT_BODY",BODY,{"disambiguationData":[OSD([sQuery(id+"F0.wireOp",EDGE,"E1")])]}),"instanceName":"1"}),"instanceName":"1"}),"instanceName":"1"}),"instanceName":"1"}),"instanceName":"1"}),"instanceName":"1"}),"instanceName":"1"});
            var Q2157;
            Q2157=makeQuery(id+"F13.opPattern","COPY",BODY,{"derivedFrom":makeQuery(id+"F11.opPattern","COPY",BODY,{"derivedFrom":makeQuery(id+"F10.opPattern","COPY",BODY,{"derivedFrom":makeQuery(id+"F7.opPattern","COPY",BODY,{"derivedFrom":makeQuery(id+"F6.opPattern","COPY",BODY,{"derivedFrom":makeQuery(id+"F5.opPattern","COPY",BODY,{"derivedFrom":makeQuery(id+"F4.opPattern","COPY",BODY,{"derivedFrom":makeQuery(id+"F2.opPattern","COPY",BODY,{"derivedFrom":makeQuery(id+"F1.opRevolve","SWEPT_BODY",BODY,{"disambiguationData":[OSD([sQuery(id+"F0.wireOp",EDGE,"E1")])]}),"instanceName":"1"}),"instanceName":"1"}),"instanceName":"1"}),"instanceName":"1"}),"instanceName":"1"}),"instanceName":"1"}),"instanceName":"1"}),"instanceName":"1"});
            var Q2158;
            Q2158=makeQuery(id+"F13.opPattern","COPY",BODY,{"derivedFrom":makeQuery(id+"F11.opPattern","COPY",BODY,{"derivedFrom":makeQuery(id+"F10.opPattern","COPY",BODY,{"derivedFrom":makeQuery(id+"F7.opPattern","COPY",BODY,{"derivedFrom":makeQuery(id+"F6.opPattern","COPY",BODY,{"derivedFrom":makeQuery(id+"F5.opPattern","COPY",BODY,{"derivedFrom":makeQuery(id+"F4.opPattern","COPY",BODY,{"derivedFrom":makeQuery(id+"F3.opPattern","COPY",BODY,{"derivedFrom":makeQuery(id+"F2.opPattern","COPY",BODY,{"derivedFrom":makeQuery(id+"F1.opRevolve","SWEPT_BODY",BODY,{"disambiguationData":[OSD([sQuery(id+"F0.wireOp",EDGE,"E1")])]}),"instanceName":"1"}),"instanceName":"1"}),"instanceName":"1"}),"instanceName":"1"}),"instanceName":"1"}),"instanceName":"1"}),"instanceName":"1"}),"instanceName":"1"}),"instanceName":"1"});
            var Q2159;
            Q2159=makeQuery(id+"F13.opPattern","COPY",BODY,{"derivedFrom":makeQuery(id+"F11.opPattern","COPY",BODY,{"derivedFrom":makeQuery(id+"F10.opPattern","COPY",BODY,{"derivedFrom":makeQuery(id+"F8.opPattern","COPY",BODY,{"derivedFrom":makeQuery(id+"F1.opRevolve","SWEPT_BODY",BODY,{"disambiguationData":[OSD([sQuery(id+"F0.wireOp",EDGE,"E1")])]}),"instanceName":"1"}),"instanceName":"1"}),"instanceName":"1"}),"instanceName":"1"});
            var Q2160;
            Q2160=makeQuery(id+"F13.opPattern","COPY",BODY,{"derivedFrom":makeQuery(id+"F11.opPattern","COPY",BODY,{"derivedFrom":makeQuery(id+"F10.opPattern","COPY",BODY,{"derivedFrom":makeQuery(id+"F8.opPattern","COPY",BODY,{"derivedFrom":makeQuery(id+"F2.opPattern","COPY",BODY,{"derivedFrom":makeQuery(id+"F1.opRevolve","SWEPT_BODY",BODY,{"disambiguationData":[OSD([sQuery(id+"F0.wireOp",EDGE,"E1")])]}),"instanceName":"1"}),"instanceName":"1"}),"instanceName":"1"}),"instanceName":"1"}),"instanceName":"1"});
            var Q2161;
            Q2161=makeQuery(id+"F13.opPattern","COPY",BODY,{"derivedFrom":makeQuery(id+"F11.opPattern","COPY",BODY,{"derivedFrom":makeQuery(id+"F10.opPattern","COPY",BODY,{"derivedFrom":makeQuery(id+"F8.opPattern","COPY",BODY,{"derivedFrom":makeQuery(id+"F3.opPattern","COPY",BODY,{"derivedFrom":makeQuery(id+"F2.opPattern","COPY",BODY,{"derivedFrom":makeQuery(id+"F1.opRevolve","SWEPT_BODY",BODY,{"disambiguationData":[OSD([sQuery(id+"F0.wireOp",EDGE,"E1")])]}),"instanceName":"1"}),"instanceName":"1"}),"instanceName":"1"}),"instanceName":"1"}),"instanceName":"1"}),"instanceName":"1"});
            var Q2162;
            Q2162=makeQuery(id+"F13.opPattern","COPY",BODY,{"derivedFrom":makeQuery(id+"F11.opPattern","COPY",BODY,{"derivedFrom":makeQuery(id+"F10.opPattern","COPY",BODY,{"derivedFrom":makeQuery(id+"F8.opPattern","COPY",BODY,{"derivedFrom":makeQuery(id+"F4.opPattern","COPY",BODY,{"derivedFrom":makeQuery(id+"F1.opRevolve","SWEPT_BODY",BODY,{"disambiguationData":[OSD([sQuery(id+"F0.wireOp",EDGE,"E1")])]}),"instanceName":"1"}),"instanceName":"1"}),"instanceName":"1"}),"instanceName":"1"}),"instanceName":"1"});
            var Q2163;
            Q2163=makeQuery(id+"F13.opPattern","COPY",BODY,{"derivedFrom":makeQuery(id+"F11.opPattern","COPY",BODY,{"derivedFrom":makeQuery(id+"F10.opPattern","COPY",BODY,{"derivedFrom":makeQuery(id+"F8.opPattern","COPY",BODY,{"derivedFrom":makeQuery(id+"F4.opPattern","COPY",BODY,{"derivedFrom":makeQuery(id+"F2.opPattern","COPY",BODY,{"derivedFrom":makeQuery(id+"F1.opRevolve","SWEPT_BODY",BODY,{"disambiguationData":[OSD([sQuery(id+"F0.wireOp",EDGE,"E1")])]}),"instanceName":"1"}),"instanceName":"1"}),"instanceName":"1"}),"instanceName":"1"}),"instanceName":"1"}),"instanceName":"1"});
            var Q2164;
            Q2164=makeQuery(id+"F13.opPattern","COPY",BODY,{"derivedFrom":makeQuery(id+"F11.opPattern","COPY",BODY,{"derivedFrom":makeQuery(id+"F10.opPattern","COPY",BODY,{"derivedFrom":makeQuery(id+"F8.opPattern","COPY",BODY,{"derivedFrom":makeQuery(id+"F4.opPattern","COPY",BODY,{"derivedFrom":makeQuery(id+"F3.opPattern","COPY",BODY,{"derivedFrom":makeQuery(id+"F2.opPattern","COPY",BODY,{"derivedFrom":makeQuery(id+"F1.opRevolve","SWEPT_BODY",BODY,{"disambiguationData":[OSD([sQuery(id+"F0.wireOp",EDGE,"E1")])]}),"instanceName":"1"}),"instanceName":"1"}),"instanceName":"1"}),"instanceName":"1"}),"instanceName":"1"}),"instanceName":"1"}),"instanceName":"1"});
            var Q2165;
            Q2165=makeQuery(id+"F13.opPattern","COPY",BODY,{"derivedFrom":makeQuery(id+"F11.opPattern","COPY",BODY,{"derivedFrom":makeQuery(id+"F10.opPattern","COPY",BODY,{"derivedFrom":makeQuery(id+"F8.opPattern","COPY",BODY,{"derivedFrom":makeQuery(id+"F5.opPattern","COPY",BODY,{"derivedFrom":makeQuery(id+"F1.opRevolve","SWEPT_BODY",BODY,{"disambiguationData":[OSD([sQuery(id+"F0.wireOp",EDGE,"E1")])]}),"instanceName":"1"}),"instanceName":"1"}),"instanceName":"1"}),"instanceName":"1"}),"instanceName":"1"});
            var Q2166;
            Q2166=makeQuery(id+"F13.opPattern","COPY",BODY,{"derivedFrom":makeQuery(id+"F11.opPattern","COPY",BODY,{"derivedFrom":makeQuery(id+"F10.opPattern","COPY",BODY,{"derivedFrom":makeQuery(id+"F8.opPattern","COPY",BODY,{"derivedFrom":makeQuery(id+"F5.opPattern","COPY",BODY,{"derivedFrom":makeQuery(id+"F2.opPattern","COPY",BODY,{"derivedFrom":makeQuery(id+"F1.opRevolve","SWEPT_BODY",BODY,{"disambiguationData":[OSD([sQuery(id+"F0.wireOp",EDGE,"E1")])]}),"instanceName":"1"}),"instanceName":"1"}),"instanceName":"1"}),"instanceName":"1"}),"instanceName":"1"}),"instanceName":"1"});
            var Q2167;
            Q2167=makeQuery(id+"F13.opPattern","COPY",BODY,{"derivedFrom":makeQuery(id+"F11.opPattern","COPY",BODY,{"derivedFrom":makeQuery(id+"F10.opPattern","COPY",BODY,{"derivedFrom":makeQuery(id+"F8.opPattern","COPY",BODY,{"derivedFrom":makeQuery(id+"F5.opPattern","COPY",BODY,{"derivedFrom":makeQuery(id+"F3.opPattern","COPY",BODY,{"derivedFrom":makeQuery(id+"F2.opPattern","COPY",BODY,{"derivedFrom":makeQuery(id+"F1.opRevolve","SWEPT_BODY",BODY,{"disambiguationData":[OSD([sQuery(id+"F0.wireOp",EDGE,"E1")])]}),"instanceName":"1"}),"instanceName":"1"}),"instanceName":"1"}),"instanceName":"1"}),"instanceName":"1"}),"instanceName":"1"}),"instanceName":"1"});
            var Q2168;
            Q2168=makeQuery(id+"F13.opPattern","COPY",BODY,{"derivedFrom":makeQuery(id+"F11.opPattern","COPY",BODY,{"derivedFrom":makeQuery(id+"F10.opPattern","COPY",BODY,{"derivedFrom":makeQuery(id+"F8.opPattern","COPY",BODY,{"derivedFrom":makeQuery(id+"F5.opPattern","COPY",BODY,{"derivedFrom":makeQuery(id+"F4.opPattern","COPY",BODY,{"derivedFrom":makeQuery(id+"F1.opRevolve","SWEPT_BODY",BODY,{"disambiguationData":[OSD([sQuery(id+"F0.wireOp",EDGE,"E1")])]}),"instanceName":"1"}),"instanceName":"1"}),"instanceName":"1"}),"instanceName":"1"}),"instanceName":"1"}),"instanceName":"1"});
            var Q2169;
            Q2169=makeQuery(id+"F13.opPattern","COPY",BODY,{"derivedFrom":makeQuery(id+"F11.opPattern","COPY",BODY,{"derivedFrom":makeQuery(id+"F10.opPattern","COPY",BODY,{"derivedFrom":makeQuery(id+"F8.opPattern","COPY",BODY,{"derivedFrom":makeQuery(id+"F5.opPattern","COPY",BODY,{"derivedFrom":makeQuery(id+"F4.opPattern","COPY",BODY,{"derivedFrom":makeQuery(id+"F2.opPattern","COPY",BODY,{"derivedFrom":makeQuery(id+"F1.opRevolve","SWEPT_BODY",BODY,{"disambiguationData":[OSD([sQuery(id+"F0.wireOp",EDGE,"E1")])]}),"instanceName":"1"}),"instanceName":"1"}),"instanceName":"1"}),"instanceName":"1"}),"instanceName":"1"}),"instanceName":"1"}),"instanceName":"1"});
            var Q2170;
            Q2170=makeQuery(id+"F13.opPattern","COPY",BODY,{"derivedFrom":makeQuery(id+"F11.opPattern","COPY",BODY,{"derivedFrom":makeQuery(id+"F10.opPattern","COPY",BODY,{"derivedFrom":makeQuery(id+"F8.opPattern","COPY",BODY,{"derivedFrom":makeQuery(id+"F5.opPattern","COPY",BODY,{"derivedFrom":makeQuery(id+"F4.opPattern","COPY",BODY,{"derivedFrom":makeQuery(id+"F3.opPattern","COPY",BODY,{"derivedFrom":makeQuery(id+"F2.opPattern","COPY",BODY,{"derivedFrom":makeQuery(id+"F1.opRevolve","SWEPT_BODY",BODY,{"disambiguationData":[OSD([sQuery(id+"F0.wireOp",EDGE,"E1")])]}),"instanceName":"1"}),"instanceName":"1"}),"instanceName":"1"}),"instanceName":"1"}),"instanceName":"1"}),"instanceName":"1"}),"instanceName":"1"}),"instanceName":"1"});
            var Q2171;
            Q2171=makeQuery(id+"F13.opPattern","COPY",BODY,{"derivedFrom":makeQuery(id+"F11.opPattern","COPY",BODY,{"derivedFrom":makeQuery(id+"F10.opPattern","COPY",BODY,{"derivedFrom":makeQuery(id+"F8.opPattern","COPY",BODY,{"derivedFrom":makeQuery(id+"F6.opPattern","COPY",BODY,{"derivedFrom":makeQuery(id+"F1.opRevolve","SWEPT_BODY",BODY,{"disambiguationData":[OSD([sQuery(id+"F0.wireOp",EDGE,"E1")])]}),"instanceName":"1"}),"instanceName":"1"}),"instanceName":"1"}),"instanceName":"1"}),"instanceName":"1"});
            var Q2172;
            Q2172=makeQuery(id+"F13.opPattern","COPY",BODY,{"derivedFrom":makeQuery(id+"F11.opPattern","COPY",BODY,{"derivedFrom":makeQuery(id+"F10.opPattern","COPY",BODY,{"derivedFrom":makeQuery(id+"F8.opPattern","COPY",BODY,{"derivedFrom":makeQuery(id+"F6.opPattern","COPY",BODY,{"derivedFrom":makeQuery(id+"F2.opPattern","COPY",BODY,{"derivedFrom":makeQuery(id+"F1.opRevolve","SWEPT_BODY",BODY,{"disambiguationData":[OSD([sQuery(id+"F0.wireOp",EDGE,"E1")])]}),"instanceName":"1"}),"instanceName":"1"}),"instanceName":"1"}),"instanceName":"1"}),"instanceName":"1"}),"instanceName":"1"});
            var Q2173;
            Q2173=makeQuery(id+"F13.opPattern","COPY",BODY,{"derivedFrom":makeQuery(id+"F11.opPattern","COPY",BODY,{"derivedFrom":makeQuery(id+"F10.opPattern","COPY",BODY,{"derivedFrom":makeQuery(id+"F8.opPattern","COPY",BODY,{"derivedFrom":makeQuery(id+"F6.opPattern","COPY",BODY,{"derivedFrom":makeQuery(id+"F3.opPattern","COPY",BODY,{"derivedFrom":makeQuery(id+"F2.opPattern","COPY",BODY,{"derivedFrom":makeQuery(id+"F1.opRevolve","SWEPT_BODY",BODY,{"disambiguationData":[OSD([sQuery(id+"F0.wireOp",EDGE,"E1")])]}),"instanceName":"1"}),"instanceName":"1"}),"instanceName":"1"}),"instanceName":"1"}),"instanceName":"1"}),"instanceName":"1"}),"instanceName":"1"});
            var Q2174;
            Q2174=makeQuery(id+"F13.opPattern","COPY",BODY,{"derivedFrom":makeQuery(id+"F11.opPattern","COPY",BODY,{"derivedFrom":makeQuery(id+"F10.opPattern","COPY",BODY,{"derivedFrom":makeQuery(id+"F8.opPattern","COPY",BODY,{"derivedFrom":makeQuery(id+"F6.opPattern","COPY",BODY,{"derivedFrom":makeQuery(id+"F4.opPattern","COPY",BODY,{"derivedFrom":makeQuery(id+"F1.opRevolve","SWEPT_BODY",BODY,{"disambiguationData":[OSD([sQuery(id+"F0.wireOp",EDGE,"E1")])]}),"instanceName":"1"}),"instanceName":"1"}),"instanceName":"1"}),"instanceName":"1"}),"instanceName":"1"}),"instanceName":"1"});
            var Q2175;
            Q2175=makeQuery(id+"F13.opPattern","COPY",BODY,{"derivedFrom":makeQuery(id+"F11.opPattern","COPY",BODY,{"derivedFrom":makeQuery(id+"F10.opPattern","COPY",BODY,{"derivedFrom":makeQuery(id+"F8.opPattern","COPY",BODY,{"derivedFrom":makeQuery(id+"F6.opPattern","COPY",BODY,{"derivedFrom":makeQuery(id+"F4.opPattern","COPY",BODY,{"derivedFrom":makeQuery(id+"F2.opPattern","COPY",BODY,{"derivedFrom":makeQuery(id+"F1.opRevolve","SWEPT_BODY",BODY,{"disambiguationData":[OSD([sQuery(id+"F0.wireOp",EDGE,"E1")])]}),"instanceName":"1"}),"instanceName":"1"}),"instanceName":"1"}),"instanceName":"1"}),"instanceName":"1"}),"instanceName":"1"}),"instanceName":"1"});
            var Q2176;
            Q2176=makeQuery(id+"F13.opPattern","COPY",BODY,{"derivedFrom":makeQuery(id+"F11.opPattern","COPY",BODY,{"derivedFrom":makeQuery(id+"F10.opPattern","COPY",BODY,{"derivedFrom":makeQuery(id+"F8.opPattern","COPY",BODY,{"derivedFrom":makeQuery(id+"F6.opPattern","COPY",BODY,{"derivedFrom":makeQuery(id+"F4.opPattern","COPY",BODY,{"derivedFrom":makeQuery(id+"F3.opPattern","COPY",BODY,{"derivedFrom":makeQuery(id+"F2.opPattern","COPY",BODY,{"derivedFrom":makeQuery(id+"F1.opRevolve","SWEPT_BODY",BODY,{"disambiguationData":[OSD([sQuery(id+"F0.wireOp",EDGE,"E1")])]}),"instanceName":"1"}),"instanceName":"1"}),"instanceName":"1"}),"instanceName":"1"}),"instanceName":"1"}),"instanceName":"1"}),"instanceName":"1"}),"instanceName":"1"});
            var Q2177;
            Q2177=makeQuery(id+"F13.opPattern","COPY",BODY,{"derivedFrom":makeQuery(id+"F11.opPattern","COPY",BODY,{"derivedFrom":makeQuery(id+"F10.opPattern","COPY",BODY,{"derivedFrom":makeQuery(id+"F8.opPattern","COPY",BODY,{"derivedFrom":makeQuery(id+"F6.opPattern","COPY",BODY,{"derivedFrom":makeQuery(id+"F5.opPattern","COPY",BODY,{"derivedFrom":makeQuery(id+"F1.opRevolve","SWEPT_BODY",BODY,{"disambiguationData":[OSD([sQuery(id+"F0.wireOp",EDGE,"E1")])]}),"instanceName":"1"}),"instanceName":"1"}),"instanceName":"1"}),"instanceName":"1"}),"instanceName":"1"}),"instanceName":"1"});
            var Q2178;
            Q2178=makeQuery(id+"F13.opPattern","COPY",BODY,{"derivedFrom":makeQuery(id+"F11.opPattern","COPY",BODY,{"derivedFrom":makeQuery(id+"F10.opPattern","COPY",BODY,{"derivedFrom":makeQuery(id+"F8.opPattern","COPY",BODY,{"derivedFrom":makeQuery(id+"F6.opPattern","COPY",BODY,{"derivedFrom":makeQuery(id+"F5.opPattern","COPY",BODY,{"derivedFrom":makeQuery(id+"F2.opPattern","COPY",BODY,{"derivedFrom":makeQuery(id+"F1.opRevolve","SWEPT_BODY",BODY,{"disambiguationData":[OSD([sQuery(id+"F0.wireOp",EDGE,"E1")])]}),"instanceName":"1"}),"instanceName":"1"}),"instanceName":"1"}),"instanceName":"1"}),"instanceName":"1"}),"instanceName":"1"}),"instanceName":"1"});
            var Q2179;
            Q2179=makeQuery(id+"F13.opPattern","COPY",BODY,{"derivedFrom":makeQuery(id+"F11.opPattern","COPY",BODY,{"derivedFrom":makeQuery(id+"F10.opPattern","COPY",BODY,{"derivedFrom":makeQuery(id+"F8.opPattern","COPY",BODY,{"derivedFrom":makeQuery(id+"F6.opPattern","COPY",BODY,{"derivedFrom":makeQuery(id+"F5.opPattern","COPY",BODY,{"derivedFrom":makeQuery(id+"F3.opPattern","COPY",BODY,{"derivedFrom":makeQuery(id+"F2.opPattern","COPY",BODY,{"derivedFrom":makeQuery(id+"F1.opRevolve","SWEPT_BODY",BODY,{"disambiguationData":[OSD([sQuery(id+"F0.wireOp",EDGE,"E1")])]}),"instanceName":"1"}),"instanceName":"1"}),"instanceName":"1"}),"instanceName":"1"}),"instanceName":"1"}),"instanceName":"1"}),"instanceName":"1"}),"instanceName":"1"});
            var Q2180;
            Q2180=makeQuery(id+"F13.opPattern","COPY",BODY,{"derivedFrom":makeQuery(id+"F11.opPattern","COPY",BODY,{"derivedFrom":makeQuery(id+"F10.opPattern","COPY",BODY,{"derivedFrom":makeQuery(id+"F8.opPattern","COPY",BODY,{"derivedFrom":makeQuery(id+"F6.opPattern","COPY",BODY,{"derivedFrom":makeQuery(id+"F5.opPattern","COPY",BODY,{"derivedFrom":makeQuery(id+"F4.opPattern","COPY",BODY,{"derivedFrom":makeQuery(id+"F1.opRevolve","SWEPT_BODY",BODY,{"disambiguationData":[OSD([sQuery(id+"F0.wireOp",EDGE,"E1")])]}),"instanceName":"1"}),"instanceName":"1"}),"instanceName":"1"}),"instanceName":"1"}),"instanceName":"1"}),"instanceName":"1"}),"instanceName":"1"});
            var Q2181;
            Q2181=makeQuery(id+"F13.opPattern","COPY",BODY,{"derivedFrom":makeQuery(id+"F11.opPattern","COPY",BODY,{"derivedFrom":makeQuery(id+"F10.opPattern","COPY",BODY,{"derivedFrom":makeQuery(id+"F8.opPattern","COPY",BODY,{"derivedFrom":makeQuery(id+"F6.opPattern","COPY",BODY,{"derivedFrom":makeQuery(id+"F5.opPattern","COPY",BODY,{"derivedFrom":makeQuery(id+"F4.opPattern","COPY",BODY,{"derivedFrom":makeQuery(id+"F2.opPattern","COPY",BODY,{"derivedFrom":makeQuery(id+"F1.opRevolve","SWEPT_BODY",BODY,{"disambiguationData":[OSD([sQuery(id+"F0.wireOp",EDGE,"E1")])]}),"instanceName":"1"}),"instanceName":"1"}),"instanceName":"1"}),"instanceName":"1"}),"instanceName":"1"}),"instanceName":"1"}),"instanceName":"1"}),"instanceName":"1"});
            var Q2182;
            Q2182=makeQuery(id+"F13.opPattern","COPY",BODY,{"derivedFrom":makeQuery(id+"F11.opPattern","COPY",BODY,{"derivedFrom":makeQuery(id+"F10.opPattern","COPY",BODY,{"derivedFrom":makeQuery(id+"F8.opPattern","COPY",BODY,{"derivedFrom":makeQuery(id+"F6.opPattern","COPY",BODY,{"derivedFrom":makeQuery(id+"F5.opPattern","COPY",BODY,{"derivedFrom":makeQuery(id+"F4.opPattern","COPY",BODY,{"derivedFrom":makeQuery(id+"F3.opPattern","COPY",BODY,{"derivedFrom":makeQuery(id+"F2.opPattern","COPY",BODY,{"derivedFrom":makeQuery(id+"F1.opRevolve","SWEPT_BODY",BODY,{"disambiguationData":[OSD([sQuery(id+"F0.wireOp",EDGE,"E1")])]}),"instanceName":"1"}),"instanceName":"1"}),"instanceName":"1"}),"instanceName":"1"}),"instanceName":"1"}),"instanceName":"1"}),"instanceName":"1"}),"instanceName":"1"}),"instanceName":"1"});
            var Q2183;
            Q2183=makeQuery(id+"F13.opPattern","COPY",BODY,{"derivedFrom":makeQuery(id+"F11.opPattern","COPY",BODY,{"derivedFrom":makeQuery(id+"F10.opPattern","COPY",BODY,{"derivedFrom":makeQuery(id+"F8.opPattern","COPY",BODY,{"derivedFrom":makeQuery(id+"F7.opPattern","COPY",BODY,{"derivedFrom":makeQuery(id+"F1.opRevolve","SWEPT_BODY",BODY,{"disambiguationData":[OSD([sQuery(id+"F0.wireOp",EDGE,"E1")])]}),"instanceName":"1"}),"instanceName":"1"}),"instanceName":"1"}),"instanceName":"1"}),"instanceName":"1"});
            var Q2184;
            Q2184=makeQuery(id+"F13.opPattern","COPY",BODY,{"derivedFrom":makeQuery(id+"F11.opPattern","COPY",BODY,{"derivedFrom":makeQuery(id+"F10.opPattern","COPY",BODY,{"derivedFrom":makeQuery(id+"F8.opPattern","COPY",BODY,{"derivedFrom":makeQuery(id+"F7.opPattern","COPY",BODY,{"derivedFrom":makeQuery(id+"F2.opPattern","COPY",BODY,{"derivedFrom":makeQuery(id+"F1.opRevolve","SWEPT_BODY",BODY,{"disambiguationData":[OSD([sQuery(id+"F0.wireOp",EDGE,"E1")])]}),"instanceName":"1"}),"instanceName":"1"}),"instanceName":"1"}),"instanceName":"1"}),"instanceName":"1"}),"instanceName":"1"});
            var Q2185;
            Q2185=makeQuery(id+"F13.opPattern","COPY",BODY,{"derivedFrom":makeQuery(id+"F11.opPattern","COPY",BODY,{"derivedFrom":makeQuery(id+"F10.opPattern","COPY",BODY,{"derivedFrom":makeQuery(id+"F8.opPattern","COPY",BODY,{"derivedFrom":makeQuery(id+"F7.opPattern","COPY",BODY,{"derivedFrom":makeQuery(id+"F3.opPattern","COPY",BODY,{"derivedFrom":makeQuery(id+"F2.opPattern","COPY",BODY,{"derivedFrom":makeQuery(id+"F1.opRevolve","SWEPT_BODY",BODY,{"disambiguationData":[OSD([sQuery(id+"F0.wireOp",EDGE,"E1")])]}),"instanceName":"1"}),"instanceName":"1"}),"instanceName":"1"}),"instanceName":"1"}),"instanceName":"1"}),"instanceName":"1"}),"instanceName":"1"});
            var Q2186;
            Q2186=makeQuery(id+"F13.opPattern","COPY",BODY,{"derivedFrom":makeQuery(id+"F11.opPattern","COPY",BODY,{"derivedFrom":makeQuery(id+"F10.opPattern","COPY",BODY,{"derivedFrom":makeQuery(id+"F8.opPattern","COPY",BODY,{"derivedFrom":makeQuery(id+"F7.opPattern","COPY",BODY,{"derivedFrom":makeQuery(id+"F4.opPattern","COPY",BODY,{"derivedFrom":makeQuery(id+"F1.opRevolve","SWEPT_BODY",BODY,{"disambiguationData":[OSD([sQuery(id+"F0.wireOp",EDGE,"E1")])]}),"instanceName":"1"}),"instanceName":"1"}),"instanceName":"1"}),"instanceName":"1"}),"instanceName":"1"}),"instanceName":"1"});
            var Q2187;
            Q2187=makeQuery(id+"F13.opPattern","COPY",BODY,{"derivedFrom":makeQuery(id+"F11.opPattern","COPY",BODY,{"derivedFrom":makeQuery(id+"F10.opPattern","COPY",BODY,{"derivedFrom":makeQuery(id+"F8.opPattern","COPY",BODY,{"derivedFrom":makeQuery(id+"F7.opPattern","COPY",BODY,{"derivedFrom":makeQuery(id+"F4.opPattern","COPY",BODY,{"derivedFrom":makeQuery(id+"F2.opPattern","COPY",BODY,{"derivedFrom":makeQuery(id+"F1.opRevolve","SWEPT_BODY",BODY,{"disambiguationData":[OSD([sQuery(id+"F0.wireOp",EDGE,"E1")])]}),"instanceName":"1"}),"instanceName":"1"}),"instanceName":"1"}),"instanceName":"1"}),"instanceName":"1"}),"instanceName":"1"}),"instanceName":"1"});
            var Q2188;
            Q2188=makeQuery(id+"F13.opPattern","COPY",BODY,{"derivedFrom":makeQuery(id+"F11.opPattern","COPY",BODY,{"derivedFrom":makeQuery(id+"F10.opPattern","COPY",BODY,{"derivedFrom":makeQuery(id+"F8.opPattern","COPY",BODY,{"derivedFrom":makeQuery(id+"F7.opPattern","COPY",BODY,{"derivedFrom":makeQuery(id+"F4.opPattern","COPY",BODY,{"derivedFrom":makeQuery(id+"F3.opPattern","COPY",BODY,{"derivedFrom":makeQuery(id+"F2.opPattern","COPY",BODY,{"derivedFrom":makeQuery(id+"F1.opRevolve","SWEPT_BODY",BODY,{"disambiguationData":[OSD([sQuery(id+"F0.wireOp",EDGE,"E1")])]}),"instanceName":"1"}),"instanceName":"1"}),"instanceName":"1"}),"instanceName":"1"}),"instanceName":"1"}),"instanceName":"1"}),"instanceName":"1"}),"instanceName":"1"});
            var Q2189;
            Q2189=makeQuery(id+"F13.opPattern","COPY",BODY,{"derivedFrom":makeQuery(id+"F11.opPattern","COPY",BODY,{"derivedFrom":makeQuery(id+"F10.opPattern","COPY",BODY,{"derivedFrom":makeQuery(id+"F8.opPattern","COPY",BODY,{"derivedFrom":makeQuery(id+"F7.opPattern","COPY",BODY,{"derivedFrom":makeQuery(id+"F5.opPattern","COPY",BODY,{"derivedFrom":makeQuery(id+"F1.opRevolve","SWEPT_BODY",BODY,{"disambiguationData":[OSD([sQuery(id+"F0.wireOp",EDGE,"E1")])]}),"instanceName":"1"}),"instanceName":"1"}),"instanceName":"1"}),"instanceName":"1"}),"instanceName":"1"}),"instanceName":"1"});
            var Q2190;
            Q2190=makeQuery(id+"F13.opPattern","COPY",BODY,{"derivedFrom":makeQuery(id+"F11.opPattern","COPY",BODY,{"derivedFrom":makeQuery(id+"F10.opPattern","COPY",BODY,{"derivedFrom":makeQuery(id+"F8.opPattern","COPY",BODY,{"derivedFrom":makeQuery(id+"F7.opPattern","COPY",BODY,{"derivedFrom":makeQuery(id+"F5.opPattern","COPY",BODY,{"derivedFrom":makeQuery(id+"F2.opPattern","COPY",BODY,{"derivedFrom":makeQuery(id+"F1.opRevolve","SWEPT_BODY",BODY,{"disambiguationData":[OSD([sQuery(id+"F0.wireOp",EDGE,"E1")])]}),"instanceName":"1"}),"instanceName":"1"}),"instanceName":"1"}),"instanceName":"1"}),"instanceName":"1"}),"instanceName":"1"}),"instanceName":"1"});
            var Q2191;
            Q2191=makeQuery(id+"F13.opPattern","COPY",BODY,{"derivedFrom":makeQuery(id+"F11.opPattern","COPY",BODY,{"derivedFrom":makeQuery(id+"F10.opPattern","COPY",BODY,{"derivedFrom":makeQuery(id+"F8.opPattern","COPY",BODY,{"derivedFrom":makeQuery(id+"F7.opPattern","COPY",BODY,{"derivedFrom":makeQuery(id+"F5.opPattern","COPY",BODY,{"derivedFrom":makeQuery(id+"F3.opPattern","COPY",BODY,{"derivedFrom":makeQuery(id+"F2.opPattern","COPY",BODY,{"derivedFrom":makeQuery(id+"F1.opRevolve","SWEPT_BODY",BODY,{"disambiguationData":[OSD([sQuery(id+"F0.wireOp",EDGE,"E1")])]}),"instanceName":"1"}),"instanceName":"1"}),"instanceName":"1"}),"instanceName":"1"}),"instanceName":"1"}),"instanceName":"1"}),"instanceName":"1"}),"instanceName":"1"});
            var Q2192;
            Q2192=makeQuery(id+"F13.opPattern","COPY",BODY,{"derivedFrom":makeQuery(id+"F11.opPattern","COPY",BODY,{"derivedFrom":makeQuery(id+"F10.opPattern","COPY",BODY,{"derivedFrom":makeQuery(id+"F8.opPattern","COPY",BODY,{"derivedFrom":makeQuery(id+"F7.opPattern","COPY",BODY,{"derivedFrom":makeQuery(id+"F5.opPattern","COPY",BODY,{"derivedFrom":makeQuery(id+"F4.opPattern","COPY",BODY,{"derivedFrom":makeQuery(id+"F1.opRevolve","SWEPT_BODY",BODY,{"disambiguationData":[OSD([sQuery(id+"F0.wireOp",EDGE,"E1")])]}),"instanceName":"1"}),"instanceName":"1"}),"instanceName":"1"}),"instanceName":"1"}),"instanceName":"1"}),"instanceName":"1"}),"instanceName":"1"});
            var Q2193;
            Q2193=makeQuery(id+"F13.opPattern","COPY",BODY,{"derivedFrom":makeQuery(id+"F11.opPattern","COPY",BODY,{"derivedFrom":makeQuery(id+"F10.opPattern","COPY",BODY,{"derivedFrom":makeQuery(id+"F8.opPattern","COPY",BODY,{"derivedFrom":makeQuery(id+"F7.opPattern","COPY",BODY,{"derivedFrom":makeQuery(id+"F5.opPattern","COPY",BODY,{"derivedFrom":makeQuery(id+"F4.opPattern","COPY",BODY,{"derivedFrom":makeQuery(id+"F2.opPattern","COPY",BODY,{"derivedFrom":makeQuery(id+"F1.opRevolve","SWEPT_BODY",BODY,{"disambiguationData":[OSD([sQuery(id+"F0.wireOp",EDGE,"E1")])]}),"instanceName":"1"}),"instanceName":"1"}),"instanceName":"1"}),"instanceName":"1"}),"instanceName":"1"}),"instanceName":"1"}),"instanceName":"1"}),"instanceName":"1"});
            var Q2194;
            Q2194=makeQuery(id+"F13.opPattern","COPY",BODY,{"derivedFrom":makeQuery(id+"F11.opPattern","COPY",BODY,{"derivedFrom":makeQuery(id+"F10.opPattern","COPY",BODY,{"derivedFrom":makeQuery(id+"F8.opPattern","COPY",BODY,{"derivedFrom":makeQuery(id+"F7.opPattern","COPY",BODY,{"derivedFrom":makeQuery(id+"F5.opPattern","COPY",BODY,{"derivedFrom":makeQuery(id+"F4.opPattern","COPY",BODY,{"derivedFrom":makeQuery(id+"F3.opPattern","COPY",BODY,{"derivedFrom":makeQuery(id+"F2.opPattern","COPY",BODY,{"derivedFrom":makeQuery(id+"F1.opRevolve","SWEPT_BODY",BODY,{"disambiguationData":[OSD([sQuery(id+"F0.wireOp",EDGE,"E1")])]}),"instanceName":"1"}),"instanceName":"1"}),"instanceName":"1"}),"instanceName":"1"}),"instanceName":"1"}),"instanceName":"1"}),"instanceName":"1"}),"instanceName":"1"}),"instanceName":"1"});
            var Q2195;
            Q2195=makeQuery(id+"F13.opPattern","COPY",BODY,{"derivedFrom":makeQuery(id+"F11.opPattern","COPY",BODY,{"derivedFrom":makeQuery(id+"F10.opPattern","COPY",BODY,{"derivedFrom":makeQuery(id+"F8.opPattern","COPY",BODY,{"derivedFrom":makeQuery(id+"F7.opPattern","COPY",BODY,{"derivedFrom":makeQuery(id+"F6.opPattern","COPY",BODY,{"derivedFrom":makeQuery(id+"F1.opRevolve","SWEPT_BODY",BODY,{"disambiguationData":[OSD([sQuery(id+"F0.wireOp",EDGE,"E1")])]}),"instanceName":"1"}),"instanceName":"1"}),"instanceName":"1"}),"instanceName":"1"}),"instanceName":"1"}),"instanceName":"1"});
            var Q2196;
            Q2196=makeQuery(id+"F13.opPattern","COPY",BODY,{"derivedFrom":makeQuery(id+"F11.opPattern","COPY",BODY,{"derivedFrom":makeQuery(id+"F10.opPattern","COPY",BODY,{"derivedFrom":makeQuery(id+"F8.opPattern","COPY",BODY,{"derivedFrom":makeQuery(id+"F7.opPattern","COPY",BODY,{"derivedFrom":makeQuery(id+"F6.opPattern","COPY",BODY,{"derivedFrom":makeQuery(id+"F2.opPattern","COPY",BODY,{"derivedFrom":makeQuery(id+"F1.opRevolve","SWEPT_BODY",BODY,{"disambiguationData":[OSD([sQuery(id+"F0.wireOp",EDGE,"E1")])]}),"instanceName":"1"}),"instanceName":"1"}),"instanceName":"1"}),"instanceName":"1"}),"instanceName":"1"}),"instanceName":"1"}),"instanceName":"1"});
            var Q2197;
            Q2197=makeQuery(id+"F13.opPattern","COPY",BODY,{"derivedFrom":makeQuery(id+"F11.opPattern","COPY",BODY,{"derivedFrom":makeQuery(id+"F10.opPattern","COPY",BODY,{"derivedFrom":makeQuery(id+"F8.opPattern","COPY",BODY,{"derivedFrom":makeQuery(id+"F7.opPattern","COPY",BODY,{"derivedFrom":makeQuery(id+"F6.opPattern","COPY",BODY,{"derivedFrom":makeQuery(id+"F3.opPattern","COPY",BODY,{"derivedFrom":makeQuery(id+"F2.opPattern","COPY",BODY,{"derivedFrom":makeQuery(id+"F1.opRevolve","SWEPT_BODY",BODY,{"disambiguationData":[OSD([sQuery(id+"F0.wireOp",EDGE,"E1")])]}),"instanceName":"1"}),"instanceName":"1"}),"instanceName":"1"}),"instanceName":"1"}),"instanceName":"1"}),"instanceName":"1"}),"instanceName":"1"}),"instanceName":"1"});
            var Q2198;
            Q2198=makeQuery(id+"F13.opPattern","COPY",BODY,{"derivedFrom":makeQuery(id+"F11.opPattern","COPY",BODY,{"derivedFrom":makeQuery(id+"F10.opPattern","COPY",BODY,{"derivedFrom":makeQuery(id+"F8.opPattern","COPY",BODY,{"derivedFrom":makeQuery(id+"F7.opPattern","COPY",BODY,{"derivedFrom":makeQuery(id+"F6.opPattern","COPY",BODY,{"derivedFrom":makeQuery(id+"F4.opPattern","COPY",BODY,{"derivedFrom":makeQuery(id+"F1.opRevolve","SWEPT_BODY",BODY,{"disambiguationData":[OSD([sQuery(id+"F0.wireOp",EDGE,"E1")])]}),"instanceName":"1"}),"instanceName":"1"}),"instanceName":"1"}),"instanceName":"1"}),"instanceName":"1"}),"instanceName":"1"}),"instanceName":"1"});
            var Q2199;
            Q2199=makeQuery(id+"F13.opPattern","COPY",BODY,{"derivedFrom":makeQuery(id+"F11.opPattern","COPY",BODY,{"derivedFrom":makeQuery(id+"F10.opPattern","COPY",BODY,{"derivedFrom":makeQuery(id+"F8.opPattern","COPY",BODY,{"derivedFrom":makeQuery(id+"F7.opPattern","COPY",BODY,{"derivedFrom":makeQuery(id+"F6.opPattern","COPY",BODY,{"derivedFrom":makeQuery(id+"F4.opPattern","COPY",BODY,{"derivedFrom":makeQuery(id+"F2.opPattern","COPY",BODY,{"derivedFrom":makeQuery(id+"F1.opRevolve","SWEPT_BODY",BODY,{"disambiguationData":[OSD([sQuery(id+"F0.wireOp",EDGE,"E1")])]}),"instanceName":"1"}),"instanceName":"1"}),"instanceName":"1"}),"instanceName":"1"}),"instanceName":"1"}),"instanceName":"1"}),"instanceName":"1"}),"instanceName":"1"});
            var Q2200;
            Q2200=makeQuery(id+"F13.opPattern","COPY",BODY,{"derivedFrom":makeQuery(id+"F11.opPattern","COPY",BODY,{"derivedFrom":makeQuery(id+"F10.opPattern","COPY",BODY,{"derivedFrom":makeQuery(id+"F8.opPattern","COPY",BODY,{"derivedFrom":makeQuery(id+"F7.opPattern","COPY",BODY,{"derivedFrom":makeQuery(id+"F6.opPattern","COPY",BODY,{"derivedFrom":makeQuery(id+"F4.opPattern","COPY",BODY,{"derivedFrom":makeQuery(id+"F3.opPattern","COPY",BODY,{"derivedFrom":makeQuery(id+"F2.opPattern","COPY",BODY,{"derivedFrom":makeQuery(id+"F1.opRevolve","SWEPT_BODY",BODY,{"disambiguationData":[OSD([sQuery(id+"F0.wireOp",EDGE,"E1")])]}),"instanceName":"1"}),"instanceName":"1"}),"instanceName":"1"}),"instanceName":"1"}),"instanceName":"1"}),"instanceName":"1"}),"instanceName":"1"}),"instanceName":"1"}),"instanceName":"1"});
            var Q2201;
            Q2201=makeQuery(id+"F13.opPattern","COPY",BODY,{"derivedFrom":makeQuery(id+"F11.opPattern","COPY",BODY,{"derivedFrom":makeQuery(id+"F10.opPattern","COPY",BODY,{"derivedFrom":makeQuery(id+"F8.opPattern","COPY",BODY,{"derivedFrom":makeQuery(id+"F7.opPattern","COPY",BODY,{"derivedFrom":makeQuery(id+"F6.opPattern","COPY",BODY,{"derivedFrom":makeQuery(id+"F5.opPattern","COPY",BODY,{"derivedFrom":makeQuery(id+"F1.opRevolve","SWEPT_BODY",BODY,{"disambiguationData":[OSD([sQuery(id+"F0.wireOp",EDGE,"E1")])]}),"instanceName":"1"}),"instanceName":"1"}),"instanceName":"1"}),"instanceName":"1"}),"instanceName":"1"}),"instanceName":"1"}),"instanceName":"1"});
            var Q2202;
            Q2202=makeQuery(id+"F13.opPattern","COPY",BODY,{"derivedFrom":makeQuery(id+"F11.opPattern","COPY",BODY,{"derivedFrom":makeQuery(id+"F10.opPattern","COPY",BODY,{"derivedFrom":makeQuery(id+"F8.opPattern","COPY",BODY,{"derivedFrom":makeQuery(id+"F7.opPattern","COPY",BODY,{"derivedFrom":makeQuery(id+"F6.opPattern","COPY",BODY,{"derivedFrom":makeQuery(id+"F5.opPattern","COPY",BODY,{"derivedFrom":makeQuery(id+"F2.opPattern","COPY",BODY,{"derivedFrom":makeQuery(id+"F1.opRevolve","SWEPT_BODY",BODY,{"disambiguationData":[OSD([sQuery(id+"F0.wireOp",EDGE,"E1")])]}),"instanceName":"1"}),"instanceName":"1"}),"instanceName":"1"}),"instanceName":"1"}),"instanceName":"1"}),"instanceName":"1"}),"instanceName":"1"}),"instanceName":"1"});
            var Q2203;
            Q2203=makeQuery(id+"F13.opPattern","COPY",BODY,{"derivedFrom":makeQuery(id+"F11.opPattern","COPY",BODY,{"derivedFrom":makeQuery(id+"F10.opPattern","COPY",BODY,{"derivedFrom":makeQuery(id+"F8.opPattern","COPY",BODY,{"derivedFrom":makeQuery(id+"F7.opPattern","COPY",BODY,{"derivedFrom":makeQuery(id+"F6.opPattern","COPY",BODY,{"derivedFrom":makeQuery(id+"F5.opPattern","COPY",BODY,{"derivedFrom":makeQuery(id+"F3.opPattern","COPY",BODY,{"derivedFrom":makeQuery(id+"F2.opPattern","COPY",BODY,{"derivedFrom":makeQuery(id+"F1.opRevolve","SWEPT_BODY",BODY,{"disambiguationData":[OSD([sQuery(id+"F0.wireOp",EDGE,"E1")])]}),"instanceName":"1"}),"instanceName":"1"}),"instanceName":"1"}),"instanceName":"1"}),"instanceName":"1"}),"instanceName":"1"}),"instanceName":"1"}),"instanceName":"1"}),"instanceName":"1"});
            var Q2204;
            Q2204=makeQuery(id+"F13.opPattern","COPY",BODY,{"derivedFrom":makeQuery(id+"F11.opPattern","COPY",BODY,{"derivedFrom":makeQuery(id+"F10.opPattern","COPY",BODY,{"derivedFrom":makeQuery(id+"F8.opPattern","COPY",BODY,{"derivedFrom":makeQuery(id+"F7.opPattern","COPY",BODY,{"derivedFrom":makeQuery(id+"F6.opPattern","COPY",BODY,{"derivedFrom":makeQuery(id+"F5.opPattern","COPY",BODY,{"derivedFrom":makeQuery(id+"F4.opPattern","COPY",BODY,{"derivedFrom":makeQuery(id+"F1.opRevolve","SWEPT_BODY",BODY,{"disambiguationData":[OSD([sQuery(id+"F0.wireOp",EDGE,"E1")])]}),"instanceName":"1"}),"instanceName":"1"}),"instanceName":"1"}),"instanceName":"1"}),"instanceName":"1"}),"instanceName":"1"}),"instanceName":"1"}),"instanceName":"1"});
            var Q2205;
            Q2205=makeQuery(id+"F13.opPattern","COPY",BODY,{"derivedFrom":makeQuery(id+"F11.opPattern","COPY",BODY,{"derivedFrom":makeQuery(id+"F10.opPattern","COPY",BODY,{"derivedFrom":makeQuery(id+"F8.opPattern","COPY",BODY,{"derivedFrom":makeQuery(id+"F7.opPattern","COPY",BODY,{"derivedFrom":makeQuery(id+"F6.opPattern","COPY",BODY,{"derivedFrom":makeQuery(id+"F5.opPattern","COPY",BODY,{"derivedFrom":makeQuery(id+"F4.opPattern","COPY",BODY,{"derivedFrom":makeQuery(id+"F2.opPattern","COPY",BODY,{"derivedFrom":makeQuery(id+"F1.opRevolve","SWEPT_BODY",BODY,{"disambiguationData":[OSD([sQuery(id+"F0.wireOp",EDGE,"E1")])]}),"instanceName":"1"}),"instanceName":"1"}),"instanceName":"1"}),"instanceName":"1"}),"instanceName":"1"}),"instanceName":"1"}),"instanceName":"1"}),"instanceName":"1"}),"instanceName":"1"});
            var Q2206;
            Q2206=makeQuery(id+"F13.opPattern","COPY",BODY,{"derivedFrom":makeQuery(id+"F11.opPattern","COPY",BODY,{"derivedFrom":makeQuery(id+"F10.opPattern","COPY",BODY,{"derivedFrom":makeQuery(id+"F8.opPattern","COPY",BODY,{"derivedFrom":makeQuery(id+"F7.opPattern","COPY",BODY,{"derivedFrom":makeQuery(id+"F6.opPattern","COPY",BODY,{"derivedFrom":makeQuery(id+"F5.opPattern","COPY",BODY,{"derivedFrom":makeQuery(id+"F4.opPattern","COPY",BODY,{"derivedFrom":makeQuery(id+"F3.opPattern","COPY",BODY,{"derivedFrom":makeQuery(id+"F2.opPattern","COPY",BODY,{"derivedFrom":makeQuery(id+"F1.opRevolve","SWEPT_BODY",BODY,{"disambiguationData":[OSD([sQuery(id+"F0.wireOp",EDGE,"E1")])]}),"instanceName":"1"}),"instanceName":"1"}),"instanceName":"1"}),"instanceName":"1"}),"instanceName":"1"}),"instanceName":"1"}),"instanceName":"1"}),"instanceName":"1"}),"instanceName":"1"}),"instanceName":"1"});
            var Q2207;
            Q2207=makeQuery(id+"F13.opPattern","COPY",BODY,{"derivedFrom":makeQuery(id+"F11.opPattern","COPY",BODY,{"derivedFrom":makeQuery(id+"F10.opPattern","COPY",BODY,{"derivedFrom":makeQuery(id+"F9.opPattern","COPY",BODY,{"derivedFrom":makeQuery(id+"F1.opRevolve","SWEPT_BODY",BODY,{"disambiguationData":[OSD([sQuery(id+"F0.wireOp",EDGE,"E1")])]}),"instanceName":"1"}),"instanceName":"1"}),"instanceName":"1"}),"instanceName":"1"});
            var Q2208;
            Q2208=makeQuery(id+"F13.opPattern","COPY",BODY,{"derivedFrom":makeQuery(id+"F11.opPattern","COPY",BODY,{"derivedFrom":makeQuery(id+"F10.opPattern","COPY",BODY,{"derivedFrom":makeQuery(id+"F9.opPattern","COPY",BODY,{"derivedFrom":makeQuery(id+"F2.opPattern","COPY",BODY,{"derivedFrom":makeQuery(id+"F1.opRevolve","SWEPT_BODY",BODY,{"disambiguationData":[OSD([sQuery(id+"F0.wireOp",EDGE,"E1")])]}),"instanceName":"1"}),"instanceName":"1"}),"instanceName":"1"}),"instanceName":"1"}),"instanceName":"1"});
            var Q2209;
            Q2209=makeQuery(id+"F13.opPattern","COPY",BODY,{"derivedFrom":makeQuery(id+"F11.opPattern","COPY",BODY,{"derivedFrom":makeQuery(id+"F10.opPattern","COPY",BODY,{"derivedFrom":makeQuery(id+"F9.opPattern","COPY",BODY,{"derivedFrom":makeQuery(id+"F3.opPattern","COPY",BODY,{"derivedFrom":makeQuery(id+"F2.opPattern","COPY",BODY,{"derivedFrom":makeQuery(id+"F1.opRevolve","SWEPT_BODY",BODY,{"disambiguationData":[OSD([sQuery(id+"F0.wireOp",EDGE,"E1")])]}),"instanceName":"1"}),"instanceName":"1"}),"instanceName":"1"}),"instanceName":"1"}),"instanceName":"1"}),"instanceName":"1"});
            var Q2210;
            Q2210=makeQuery(id+"F13.opPattern","COPY",BODY,{"derivedFrom":makeQuery(id+"F11.opPattern","COPY",BODY,{"derivedFrom":makeQuery(id+"F10.opPattern","COPY",BODY,{"derivedFrom":makeQuery(id+"F9.opPattern","COPY",BODY,{"derivedFrom":makeQuery(id+"F4.opPattern","COPY",BODY,{"derivedFrom":makeQuery(id+"F1.opRevolve","SWEPT_BODY",BODY,{"disambiguationData":[OSD([sQuery(id+"F0.wireOp",EDGE,"E1")])]}),"instanceName":"1"}),"instanceName":"1"}),"instanceName":"1"}),"instanceName":"1"}),"instanceName":"1"});
            var Q2211;
            Q2211=makeQuery(id+"F13.opPattern","COPY",BODY,{"derivedFrom":makeQuery(id+"F11.opPattern","COPY",BODY,{"derivedFrom":makeQuery(id+"F10.opPattern","COPY",BODY,{"derivedFrom":makeQuery(id+"F9.opPattern","COPY",BODY,{"derivedFrom":makeQuery(id+"F4.opPattern","COPY",BODY,{"derivedFrom":makeQuery(id+"F2.opPattern","COPY",BODY,{"derivedFrom":makeQuery(id+"F1.opRevolve","SWEPT_BODY",BODY,{"disambiguationData":[OSD([sQuery(id+"F0.wireOp",EDGE,"E1")])]}),"instanceName":"1"}),"instanceName":"1"}),"instanceName":"1"}),"instanceName":"1"}),"instanceName":"1"}),"instanceName":"1"});
            var Q2212;
            Q2212=makeQuery(id+"F13.opPattern","COPY",BODY,{"derivedFrom":makeQuery(id+"F11.opPattern","COPY",BODY,{"derivedFrom":makeQuery(id+"F10.opPattern","COPY",BODY,{"derivedFrom":makeQuery(id+"F9.opPattern","COPY",BODY,{"derivedFrom":makeQuery(id+"F4.opPattern","COPY",BODY,{"derivedFrom":makeQuery(id+"F3.opPattern","COPY",BODY,{"derivedFrom":makeQuery(id+"F2.opPattern","COPY",BODY,{"derivedFrom":makeQuery(id+"F1.opRevolve","SWEPT_BODY",BODY,{"disambiguationData":[OSD([sQuery(id+"F0.wireOp",EDGE,"E1")])]}),"instanceName":"1"}),"instanceName":"1"}),"instanceName":"1"}),"instanceName":"1"}),"instanceName":"1"}),"instanceName":"1"}),"instanceName":"1"});
            var Q2213;
            Q2213=makeQuery(id+"F13.opPattern","COPY",BODY,{"derivedFrom":makeQuery(id+"F11.opPattern","COPY",BODY,{"derivedFrom":makeQuery(id+"F10.opPattern","COPY",BODY,{"derivedFrom":makeQuery(id+"F9.opPattern","COPY",BODY,{"derivedFrom":makeQuery(id+"F5.opPattern","COPY",BODY,{"derivedFrom":makeQuery(id+"F1.opRevolve","SWEPT_BODY",BODY,{"disambiguationData":[OSD([sQuery(id+"F0.wireOp",EDGE,"E1")])]}),"instanceName":"1"}),"instanceName":"1"}),"instanceName":"1"}),"instanceName":"1"}),"instanceName":"1"});
            var Q2214;
            Q2214=makeQuery(id+"F13.opPattern","COPY",BODY,{"derivedFrom":makeQuery(id+"F11.opPattern","COPY",BODY,{"derivedFrom":makeQuery(id+"F10.opPattern","COPY",BODY,{"derivedFrom":makeQuery(id+"F9.opPattern","COPY",BODY,{"derivedFrom":makeQuery(id+"F5.opPattern","COPY",BODY,{"derivedFrom":makeQuery(id+"F2.opPattern","COPY",BODY,{"derivedFrom":makeQuery(id+"F1.opRevolve","SWEPT_BODY",BODY,{"disambiguationData":[OSD([sQuery(id+"F0.wireOp",EDGE,"E1")])]}),"instanceName":"1"}),"instanceName":"1"}),"instanceName":"1"}),"instanceName":"1"}),"instanceName":"1"}),"instanceName":"1"});
            var Q2215;
            Q2215=makeQuery(id+"F13.opPattern","COPY",BODY,{"derivedFrom":makeQuery(id+"F11.opPattern","COPY",BODY,{"derivedFrom":makeQuery(id+"F10.opPattern","COPY",BODY,{"derivedFrom":makeQuery(id+"F9.opPattern","COPY",BODY,{"derivedFrom":makeQuery(id+"F5.opPattern","COPY",BODY,{"derivedFrom":makeQuery(id+"F3.opPattern","COPY",BODY,{"derivedFrom":makeQuery(id+"F2.opPattern","COPY",BODY,{"derivedFrom":makeQuery(id+"F1.opRevolve","SWEPT_BODY",BODY,{"disambiguationData":[OSD([sQuery(id+"F0.wireOp",EDGE,"E1")])]}),"instanceName":"1"}),"instanceName":"1"}),"instanceName":"1"}),"instanceName":"1"}),"instanceName":"1"}),"instanceName":"1"}),"instanceName":"1"});
            var Q2216;
            Q2216=makeQuery(id+"F13.opPattern","COPY",BODY,{"derivedFrom":makeQuery(id+"F11.opPattern","COPY",BODY,{"derivedFrom":makeQuery(id+"F10.opPattern","COPY",BODY,{"derivedFrom":makeQuery(id+"F9.opPattern","COPY",BODY,{"derivedFrom":makeQuery(id+"F5.opPattern","COPY",BODY,{"derivedFrom":makeQuery(id+"F4.opPattern","COPY",BODY,{"derivedFrom":makeQuery(id+"F1.opRevolve","SWEPT_BODY",BODY,{"disambiguationData":[OSD([sQuery(id+"F0.wireOp",EDGE,"E1")])]}),"instanceName":"1"}),"instanceName":"1"}),"instanceName":"1"}),"instanceName":"1"}),"instanceName":"1"}),"instanceName":"1"});
            var Q2217;
            Q2217=makeQuery(id+"F13.opPattern","COPY",BODY,{"derivedFrom":makeQuery(id+"F11.opPattern","COPY",BODY,{"derivedFrom":makeQuery(id+"F10.opPattern","COPY",BODY,{"derivedFrom":makeQuery(id+"F9.opPattern","COPY",BODY,{"derivedFrom":makeQuery(id+"F5.opPattern","COPY",BODY,{"derivedFrom":makeQuery(id+"F4.opPattern","COPY",BODY,{"derivedFrom":makeQuery(id+"F2.opPattern","COPY",BODY,{"derivedFrom":makeQuery(id+"F1.opRevolve","SWEPT_BODY",BODY,{"disambiguationData":[OSD([sQuery(id+"F0.wireOp",EDGE,"E1")])]}),"instanceName":"1"}),"instanceName":"1"}),"instanceName":"1"}),"instanceName":"1"}),"instanceName":"1"}),"instanceName":"1"}),"instanceName":"1"});
            var Q2218;
            Q2218=makeQuery(id+"F13.opPattern","COPY",BODY,{"derivedFrom":makeQuery(id+"F11.opPattern","COPY",BODY,{"derivedFrom":makeQuery(id+"F10.opPattern","COPY",BODY,{"derivedFrom":makeQuery(id+"F9.opPattern","COPY",BODY,{"derivedFrom":makeQuery(id+"F5.opPattern","COPY",BODY,{"derivedFrom":makeQuery(id+"F4.opPattern","COPY",BODY,{"derivedFrom":makeQuery(id+"F3.opPattern","COPY",BODY,{"derivedFrom":makeQuery(id+"F2.opPattern","COPY",BODY,{"derivedFrom":makeQuery(id+"F1.opRevolve","SWEPT_BODY",BODY,{"disambiguationData":[OSD([sQuery(id+"F0.wireOp",EDGE,"E1")])]}),"instanceName":"1"}),"instanceName":"1"}),"instanceName":"1"}),"instanceName":"1"}),"instanceName":"1"}),"instanceName":"1"}),"instanceName":"1"}),"instanceName":"1"});
            var Q2219;
            Q2219=makeQuery(id+"F13.opPattern","COPY",BODY,{"derivedFrom":makeQuery(id+"F11.opPattern","COPY",BODY,{"derivedFrom":makeQuery(id+"F10.opPattern","COPY",BODY,{"derivedFrom":makeQuery(id+"F9.opPattern","COPY",BODY,{"derivedFrom":makeQuery(id+"F6.opPattern","COPY",BODY,{"derivedFrom":makeQuery(id+"F1.opRevolve","SWEPT_BODY",BODY,{"disambiguationData":[OSD([sQuery(id+"F0.wireOp",EDGE,"E1")])]}),"instanceName":"1"}),"instanceName":"1"}),"instanceName":"1"}),"instanceName":"1"}),"instanceName":"1"});
            var Q2220;
            Q2220=makeQuery(id+"F13.opPattern","COPY",BODY,{"derivedFrom":makeQuery(id+"F11.opPattern","COPY",BODY,{"derivedFrom":makeQuery(id+"F10.opPattern","COPY",BODY,{"derivedFrom":makeQuery(id+"F9.opPattern","COPY",BODY,{"derivedFrom":makeQuery(id+"F6.opPattern","COPY",BODY,{"derivedFrom":makeQuery(id+"F2.opPattern","COPY",BODY,{"derivedFrom":makeQuery(id+"F1.opRevolve","SWEPT_BODY",BODY,{"disambiguationData":[OSD([sQuery(id+"F0.wireOp",EDGE,"E1")])]}),"instanceName":"1"}),"instanceName":"1"}),"instanceName":"1"}),"instanceName":"1"}),"instanceName":"1"}),"instanceName":"1"});
            var Q2221;
            Q2221=makeQuery(id+"F13.opPattern","COPY",BODY,{"derivedFrom":makeQuery(id+"F11.opPattern","COPY",BODY,{"derivedFrom":makeQuery(id+"F10.opPattern","COPY",BODY,{"derivedFrom":makeQuery(id+"F9.opPattern","COPY",BODY,{"derivedFrom":makeQuery(id+"F6.opPattern","COPY",BODY,{"derivedFrom":makeQuery(id+"F3.opPattern","COPY",BODY,{"derivedFrom":makeQuery(id+"F2.opPattern","COPY",BODY,{"derivedFrom":makeQuery(id+"F1.opRevolve","SWEPT_BODY",BODY,{"disambiguationData":[OSD([sQuery(id+"F0.wireOp",EDGE,"E1")])]}),"instanceName":"1"}),"instanceName":"1"}),"instanceName":"1"}),"instanceName":"1"}),"instanceName":"1"}),"instanceName":"1"}),"instanceName":"1"});
            var Q2222;
            Q2222=makeQuery(id+"F13.opPattern","COPY",BODY,{"derivedFrom":makeQuery(id+"F11.opPattern","COPY",BODY,{"derivedFrom":makeQuery(id+"F10.opPattern","COPY",BODY,{"derivedFrom":makeQuery(id+"F9.opPattern","COPY",BODY,{"derivedFrom":makeQuery(id+"F6.opPattern","COPY",BODY,{"derivedFrom":makeQuery(id+"F4.opPattern","COPY",BODY,{"derivedFrom":makeQuery(id+"F1.opRevolve","SWEPT_BODY",BODY,{"disambiguationData":[OSD([sQuery(id+"F0.wireOp",EDGE,"E1")])]}),"instanceName":"1"}),"instanceName":"1"}),"instanceName":"1"}),"instanceName":"1"}),"instanceName":"1"}),"instanceName":"1"});
            var Q2223;
            Q2223=makeQuery(id+"F13.opPattern","COPY",BODY,{"derivedFrom":makeQuery(id+"F11.opPattern","COPY",BODY,{"derivedFrom":makeQuery(id+"F10.opPattern","COPY",BODY,{"derivedFrom":makeQuery(id+"F9.opPattern","COPY",BODY,{"derivedFrom":makeQuery(id+"F6.opPattern","COPY",BODY,{"derivedFrom":makeQuery(id+"F4.opPattern","COPY",BODY,{"derivedFrom":makeQuery(id+"F2.opPattern","COPY",BODY,{"derivedFrom":makeQuery(id+"F1.opRevolve","SWEPT_BODY",BODY,{"disambiguationData":[OSD([sQuery(id+"F0.wireOp",EDGE,"E1")])]}),"instanceName":"1"}),"instanceName":"1"}),"instanceName":"1"}),"instanceName":"1"}),"instanceName":"1"}),"instanceName":"1"}),"instanceName":"1"});
            var Q2224;
            Q2224=makeQuery(id+"F13.opPattern","COPY",BODY,{"derivedFrom":makeQuery(id+"F11.opPattern","COPY",BODY,{"derivedFrom":makeQuery(id+"F10.opPattern","COPY",BODY,{"derivedFrom":makeQuery(id+"F9.opPattern","COPY",BODY,{"derivedFrom":makeQuery(id+"F6.opPattern","COPY",BODY,{"derivedFrom":makeQuery(id+"F4.opPattern","COPY",BODY,{"derivedFrom":makeQuery(id+"F3.opPattern","COPY",BODY,{"derivedFrom":makeQuery(id+"F2.opPattern","COPY",BODY,{"derivedFrom":makeQuery(id+"F1.opRevolve","SWEPT_BODY",BODY,{"disambiguationData":[OSD([sQuery(id+"F0.wireOp",EDGE,"E1")])]}),"instanceName":"1"}),"instanceName":"1"}),"instanceName":"1"}),"instanceName":"1"}),"instanceName":"1"}),"instanceName":"1"}),"instanceName":"1"}),"instanceName":"1"});
            var Q2225;
            Q2225=makeQuery(id+"F13.opPattern","COPY",BODY,{"derivedFrom":makeQuery(id+"F11.opPattern","COPY",BODY,{"derivedFrom":makeQuery(id+"F10.opPattern","COPY",BODY,{"derivedFrom":makeQuery(id+"F9.opPattern","COPY",BODY,{"derivedFrom":makeQuery(id+"F6.opPattern","COPY",BODY,{"derivedFrom":makeQuery(id+"F5.opPattern","COPY",BODY,{"derivedFrom":makeQuery(id+"F1.opRevolve","SWEPT_BODY",BODY,{"disambiguationData":[OSD([sQuery(id+"F0.wireOp",EDGE,"E1")])]}),"instanceName":"1"}),"instanceName":"1"}),"instanceName":"1"}),"instanceName":"1"}),"instanceName":"1"}),"instanceName":"1"});
            var Q2226;
            Q2226=makeQuery(id+"F13.opPattern","COPY",BODY,{"derivedFrom":makeQuery(id+"F11.opPattern","COPY",BODY,{"derivedFrom":makeQuery(id+"F10.opPattern","COPY",BODY,{"derivedFrom":makeQuery(id+"F9.opPattern","COPY",BODY,{"derivedFrom":makeQuery(id+"F6.opPattern","COPY",BODY,{"derivedFrom":makeQuery(id+"F5.opPattern","COPY",BODY,{"derivedFrom":makeQuery(id+"F2.opPattern","COPY",BODY,{"derivedFrom":makeQuery(id+"F1.opRevolve","SWEPT_BODY",BODY,{"disambiguationData":[OSD([sQuery(id+"F0.wireOp",EDGE,"E1")])]}),"instanceName":"1"}),"instanceName":"1"}),"instanceName":"1"}),"instanceName":"1"}),"instanceName":"1"}),"instanceName":"1"}),"instanceName":"1"});
            var Q2227;
            Q2227=makeQuery(id+"F13.opPattern","COPY",BODY,{"derivedFrom":makeQuery(id+"F11.opPattern","COPY",BODY,{"derivedFrom":makeQuery(id+"F10.opPattern","COPY",BODY,{"derivedFrom":makeQuery(id+"F9.opPattern","COPY",BODY,{"derivedFrom":makeQuery(id+"F6.opPattern","COPY",BODY,{"derivedFrom":makeQuery(id+"F5.opPattern","COPY",BODY,{"derivedFrom":makeQuery(id+"F3.opPattern","COPY",BODY,{"derivedFrom":makeQuery(id+"F2.opPattern","COPY",BODY,{"derivedFrom":makeQuery(id+"F1.opRevolve","SWEPT_BODY",BODY,{"disambiguationData":[OSD([sQuery(id+"F0.wireOp",EDGE,"E1")])]}),"instanceName":"1"}),"instanceName":"1"}),"instanceName":"1"}),"instanceName":"1"}),"instanceName":"1"}),"instanceName":"1"}),"instanceName":"1"}),"instanceName":"1"});
            var Q2228;
            Q2228=makeQuery(id+"F13.opPattern","COPY",BODY,{"derivedFrom":makeQuery(id+"F11.opPattern","COPY",BODY,{"derivedFrom":makeQuery(id+"F10.opPattern","COPY",BODY,{"derivedFrom":makeQuery(id+"F9.opPattern","COPY",BODY,{"derivedFrom":makeQuery(id+"F6.opPattern","COPY",BODY,{"derivedFrom":makeQuery(id+"F5.opPattern","COPY",BODY,{"derivedFrom":makeQuery(id+"F4.opPattern","COPY",BODY,{"derivedFrom":makeQuery(id+"F1.opRevolve","SWEPT_BODY",BODY,{"disambiguationData":[OSD([sQuery(id+"F0.wireOp",EDGE,"E1")])]}),"instanceName":"1"}),"instanceName":"1"}),"instanceName":"1"}),"instanceName":"1"}),"instanceName":"1"}),"instanceName":"1"}),"instanceName":"1"});
            var Q2229;
            Q2229=makeQuery(id+"F13.opPattern","COPY",BODY,{"derivedFrom":makeQuery(id+"F11.opPattern","COPY",BODY,{"derivedFrom":makeQuery(id+"F10.opPattern","COPY",BODY,{"derivedFrom":makeQuery(id+"F9.opPattern","COPY",BODY,{"derivedFrom":makeQuery(id+"F6.opPattern","COPY",BODY,{"derivedFrom":makeQuery(id+"F5.opPattern","COPY",BODY,{"derivedFrom":makeQuery(id+"F4.opPattern","COPY",BODY,{"derivedFrom":makeQuery(id+"F2.opPattern","COPY",BODY,{"derivedFrom":makeQuery(id+"F1.opRevolve","SWEPT_BODY",BODY,{"disambiguationData":[OSD([sQuery(id+"F0.wireOp",EDGE,"E1")])]}),"instanceName":"1"}),"instanceName":"1"}),"instanceName":"1"}),"instanceName":"1"}),"instanceName":"1"}),"instanceName":"1"}),"instanceName":"1"}),"instanceName":"1"});
            var Q2230;
            Q2230=makeQuery(id+"F13.opPattern","COPY",BODY,{"derivedFrom":makeQuery(id+"F11.opPattern","COPY",BODY,{"derivedFrom":makeQuery(id+"F10.opPattern","COPY",BODY,{"derivedFrom":makeQuery(id+"F9.opPattern","COPY",BODY,{"derivedFrom":makeQuery(id+"F6.opPattern","COPY",BODY,{"derivedFrom":makeQuery(id+"F5.opPattern","COPY",BODY,{"derivedFrom":makeQuery(id+"F4.opPattern","COPY",BODY,{"derivedFrom":makeQuery(id+"F3.opPattern","COPY",BODY,{"derivedFrom":makeQuery(id+"F2.opPattern","COPY",BODY,{"derivedFrom":makeQuery(id+"F1.opRevolve","SWEPT_BODY",BODY,{"disambiguationData":[OSD([sQuery(id+"F0.wireOp",EDGE,"E1")])]}),"instanceName":"1"}),"instanceName":"1"}),"instanceName":"1"}),"instanceName":"1"}),"instanceName":"1"}),"instanceName":"1"}),"instanceName":"1"}),"instanceName":"1"}),"instanceName":"1"});
            var Q2231;
            Q2231=makeQuery(id+"F13.opPattern","COPY",BODY,{"derivedFrom":makeQuery(id+"F11.opPattern","COPY",BODY,{"derivedFrom":makeQuery(id+"F10.opPattern","COPY",BODY,{"derivedFrom":makeQuery(id+"F9.opPattern","COPY",BODY,{"derivedFrom":makeQuery(id+"F7.opPattern","COPY",BODY,{"derivedFrom":makeQuery(id+"F1.opRevolve","SWEPT_BODY",BODY,{"disambiguationData":[OSD([sQuery(id+"F0.wireOp",EDGE,"E1")])]}),"instanceName":"1"}),"instanceName":"1"}),"instanceName":"1"}),"instanceName":"1"}),"instanceName":"1"});
            var Q2232;
            Q2232=makeQuery(id+"F13.opPattern","COPY",BODY,{"derivedFrom":makeQuery(id+"F11.opPattern","COPY",BODY,{"derivedFrom":makeQuery(id+"F10.opPattern","COPY",BODY,{"derivedFrom":makeQuery(id+"F9.opPattern","COPY",BODY,{"derivedFrom":makeQuery(id+"F7.opPattern","COPY",BODY,{"derivedFrom":makeQuery(id+"F2.opPattern","COPY",BODY,{"derivedFrom":makeQuery(id+"F1.opRevolve","SWEPT_BODY",BODY,{"disambiguationData":[OSD([sQuery(id+"F0.wireOp",EDGE,"E1")])]}),"instanceName":"1"}),"instanceName":"1"}),"instanceName":"1"}),"instanceName":"1"}),"instanceName":"1"}),"instanceName":"1"});
            var Q2233;
            Q2233=makeQuery(id+"F13.opPattern","COPY",BODY,{"derivedFrom":makeQuery(id+"F11.opPattern","COPY",BODY,{"derivedFrom":makeQuery(id+"F10.opPattern","COPY",BODY,{"derivedFrom":makeQuery(id+"F9.opPattern","COPY",BODY,{"derivedFrom":makeQuery(id+"F7.opPattern","COPY",BODY,{"derivedFrom":makeQuery(id+"F3.opPattern","COPY",BODY,{"derivedFrom":makeQuery(id+"F2.opPattern","COPY",BODY,{"derivedFrom":makeQuery(id+"F1.opRevolve","SWEPT_BODY",BODY,{"disambiguationData":[OSD([sQuery(id+"F0.wireOp",EDGE,"E1")])]}),"instanceName":"1"}),"instanceName":"1"}),"instanceName":"1"}),"instanceName":"1"}),"instanceName":"1"}),"instanceName":"1"}),"instanceName":"1"});
            var Q2234;
            Q2234=makeQuery(id+"F13.opPattern","COPY",BODY,{"derivedFrom":makeQuery(id+"F11.opPattern","COPY",BODY,{"derivedFrom":makeQuery(id+"F10.opPattern","COPY",BODY,{"derivedFrom":makeQuery(id+"F9.opPattern","COPY",BODY,{"derivedFrom":makeQuery(id+"F7.opPattern","COPY",BODY,{"derivedFrom":makeQuery(id+"F4.opPattern","COPY",BODY,{"derivedFrom":makeQuery(id+"F1.opRevolve","SWEPT_BODY",BODY,{"disambiguationData":[OSD([sQuery(id+"F0.wireOp",EDGE,"E1")])]}),"instanceName":"1"}),"instanceName":"1"}),"instanceName":"1"}),"instanceName":"1"}),"instanceName":"1"}),"instanceName":"1"});
            var Q2235;
            Q2235=makeQuery(id+"F13.opPattern","COPY",BODY,{"derivedFrom":makeQuery(id+"F11.opPattern","COPY",BODY,{"derivedFrom":makeQuery(id+"F10.opPattern","COPY",BODY,{"derivedFrom":makeQuery(id+"F9.opPattern","COPY",BODY,{"derivedFrom":makeQuery(id+"F7.opPattern","COPY",BODY,{"derivedFrom":makeQuery(id+"F4.opPattern","COPY",BODY,{"derivedFrom":makeQuery(id+"F2.opPattern","COPY",BODY,{"derivedFrom":makeQuery(id+"F1.opRevolve","SWEPT_BODY",BODY,{"disambiguationData":[OSD([sQuery(id+"F0.wireOp",EDGE,"E1")])]}),"instanceName":"1"}),"instanceName":"1"}),"instanceName":"1"}),"instanceName":"1"}),"instanceName":"1"}),"instanceName":"1"}),"instanceName":"1"});
            var Q2236;
            Q2236=makeQuery(id+"F13.opPattern","COPY",BODY,{"derivedFrom":makeQuery(id+"F11.opPattern","COPY",BODY,{"derivedFrom":makeQuery(id+"F10.opPattern","COPY",BODY,{"derivedFrom":makeQuery(id+"F9.opPattern","COPY",BODY,{"derivedFrom":makeQuery(id+"F7.opPattern","COPY",BODY,{"derivedFrom":makeQuery(id+"F4.opPattern","COPY",BODY,{"derivedFrom":makeQuery(id+"F3.opPattern","COPY",BODY,{"derivedFrom":makeQuery(id+"F2.opPattern","COPY",BODY,{"derivedFrom":makeQuery(id+"F1.opRevolve","SWEPT_BODY",BODY,{"disambiguationData":[OSD([sQuery(id+"F0.wireOp",EDGE,"E1")])]}),"instanceName":"1"}),"instanceName":"1"}),"instanceName":"1"}),"instanceName":"1"}),"instanceName":"1"}),"instanceName":"1"}),"instanceName":"1"}),"instanceName":"1"});
            var Q2237;
            Q2237=makeQuery(id+"F13.opPattern","COPY",BODY,{"derivedFrom":makeQuery(id+"F11.opPattern","COPY",BODY,{"derivedFrom":makeQuery(id+"F10.opPattern","COPY",BODY,{"derivedFrom":makeQuery(id+"F9.opPattern","COPY",BODY,{"derivedFrom":makeQuery(id+"F7.opPattern","COPY",BODY,{"derivedFrom":makeQuery(id+"F5.opPattern","COPY",BODY,{"derivedFrom":makeQuery(id+"F1.opRevolve","SWEPT_BODY",BODY,{"disambiguationData":[OSD([sQuery(id+"F0.wireOp",EDGE,"E1")])]}),"instanceName":"1"}),"instanceName":"1"}),"instanceName":"1"}),"instanceName":"1"}),"instanceName":"1"}),"instanceName":"1"});
            var Q2238;
            Q2238=makeQuery(id+"F13.opPattern","COPY",BODY,{"derivedFrom":makeQuery(id+"F11.opPattern","COPY",BODY,{"derivedFrom":makeQuery(id+"F10.opPattern","COPY",BODY,{"derivedFrom":makeQuery(id+"F9.opPattern","COPY",BODY,{"derivedFrom":makeQuery(id+"F7.opPattern","COPY",BODY,{"derivedFrom":makeQuery(id+"F5.opPattern","COPY",BODY,{"derivedFrom":makeQuery(id+"F2.opPattern","COPY",BODY,{"derivedFrom":makeQuery(id+"F1.opRevolve","SWEPT_BODY",BODY,{"disambiguationData":[OSD([sQuery(id+"F0.wireOp",EDGE,"E1")])]}),"instanceName":"1"}),"instanceName":"1"}),"instanceName":"1"}),"instanceName":"1"}),"instanceName":"1"}),"instanceName":"1"}),"instanceName":"1"});
            var Q2239;
            Q2239=makeQuery(id+"F13.opPattern","COPY",BODY,{"derivedFrom":makeQuery(id+"F11.opPattern","COPY",BODY,{"derivedFrom":makeQuery(id+"F10.opPattern","COPY",BODY,{"derivedFrom":makeQuery(id+"F9.opPattern","COPY",BODY,{"derivedFrom":makeQuery(id+"F7.opPattern","COPY",BODY,{"derivedFrom":makeQuery(id+"F5.opPattern","COPY",BODY,{"derivedFrom":makeQuery(id+"F3.opPattern","COPY",BODY,{"derivedFrom":makeQuery(id+"F2.opPattern","COPY",BODY,{"derivedFrom":makeQuery(id+"F1.opRevolve","SWEPT_BODY",BODY,{"disambiguationData":[OSD([sQuery(id+"F0.wireOp",EDGE,"E1")])]}),"instanceName":"1"}),"instanceName":"1"}),"instanceName":"1"}),"instanceName":"1"}),"instanceName":"1"}),"instanceName":"1"}),"instanceName":"1"}),"instanceName":"1"});
            var Q2240;
            Q2240=makeQuery(id+"F13.opPattern","COPY",BODY,{"derivedFrom":makeQuery(id+"F11.opPattern","COPY",BODY,{"derivedFrom":makeQuery(id+"F10.opPattern","COPY",BODY,{"derivedFrom":makeQuery(id+"F9.opPattern","COPY",BODY,{"derivedFrom":makeQuery(id+"F7.opPattern","COPY",BODY,{"derivedFrom":makeQuery(id+"F5.opPattern","COPY",BODY,{"derivedFrom":makeQuery(id+"F4.opPattern","COPY",BODY,{"derivedFrom":makeQuery(id+"F1.opRevolve","SWEPT_BODY",BODY,{"disambiguationData":[OSD([sQuery(id+"F0.wireOp",EDGE,"E1")])]}),"instanceName":"1"}),"instanceName":"1"}),"instanceName":"1"}),"instanceName":"1"}),"instanceName":"1"}),"instanceName":"1"}),"instanceName":"1"});
            var Q2241;
            Q2241=makeQuery(id+"F13.opPattern","COPY",BODY,{"derivedFrom":makeQuery(id+"F11.opPattern","COPY",BODY,{"derivedFrom":makeQuery(id+"F10.opPattern","COPY",BODY,{"derivedFrom":makeQuery(id+"F9.opPattern","COPY",BODY,{"derivedFrom":makeQuery(id+"F7.opPattern","COPY",BODY,{"derivedFrom":makeQuery(id+"F5.opPattern","COPY",BODY,{"derivedFrom":makeQuery(id+"F4.opPattern","COPY",BODY,{"derivedFrom":makeQuery(id+"F2.opPattern","COPY",BODY,{"derivedFrom":makeQuery(id+"F1.opRevolve","SWEPT_BODY",BODY,{"disambiguationData":[OSD([sQuery(id+"F0.wireOp",EDGE,"E1")])]}),"instanceName":"1"}),"instanceName":"1"}),"instanceName":"1"}),"instanceName":"1"}),"instanceName":"1"}),"instanceName":"1"}),"instanceName":"1"}),"instanceName":"1"});
            var Q2242;
            Q2242=makeQuery(id+"F13.opPattern","COPY",BODY,{"derivedFrom":makeQuery(id+"F11.opPattern","COPY",BODY,{"derivedFrom":makeQuery(id+"F10.opPattern","COPY",BODY,{"derivedFrom":makeQuery(id+"F9.opPattern","COPY",BODY,{"derivedFrom":makeQuery(id+"F7.opPattern","COPY",BODY,{"derivedFrom":makeQuery(id+"F5.opPattern","COPY",BODY,{"derivedFrom":makeQuery(id+"F4.opPattern","COPY",BODY,{"derivedFrom":makeQuery(id+"F3.opPattern","COPY",BODY,{"derivedFrom":makeQuery(id+"F2.opPattern","COPY",BODY,{"derivedFrom":makeQuery(id+"F1.opRevolve","SWEPT_BODY",BODY,{"disambiguationData":[OSD([sQuery(id+"F0.wireOp",EDGE,"E1")])]}),"instanceName":"1"}),"instanceName":"1"}),"instanceName":"1"}),"instanceName":"1"}),"instanceName":"1"}),"instanceName":"1"}),"instanceName":"1"}),"instanceName":"1"}),"instanceName":"1"});
            var Q2243;
            Q2243=makeQuery(id+"F13.opPattern","COPY",BODY,{"derivedFrom":makeQuery(id+"F11.opPattern","COPY",BODY,{"derivedFrom":makeQuery(id+"F10.opPattern","COPY",BODY,{"derivedFrom":makeQuery(id+"F9.opPattern","COPY",BODY,{"derivedFrom":makeQuery(id+"F7.opPattern","COPY",BODY,{"derivedFrom":makeQuery(id+"F6.opPattern","COPY",BODY,{"derivedFrom":makeQuery(id+"F1.opRevolve","SWEPT_BODY",BODY,{"disambiguationData":[OSD([sQuery(id+"F0.wireOp",EDGE,"E1")])]}),"instanceName":"1"}),"instanceName":"1"}),"instanceName":"1"}),"instanceName":"1"}),"instanceName":"1"}),"instanceName":"1"});
            var Q2244;
            Q2244=makeQuery(id+"F13.opPattern","COPY",BODY,{"derivedFrom":makeQuery(id+"F11.opPattern","COPY",BODY,{"derivedFrom":makeQuery(id+"F10.opPattern","COPY",BODY,{"derivedFrom":makeQuery(id+"F9.opPattern","COPY",BODY,{"derivedFrom":makeQuery(id+"F7.opPattern","COPY",BODY,{"derivedFrom":makeQuery(id+"F6.opPattern","COPY",BODY,{"derivedFrom":makeQuery(id+"F2.opPattern","COPY",BODY,{"derivedFrom":makeQuery(id+"F1.opRevolve","SWEPT_BODY",BODY,{"disambiguationData":[OSD([sQuery(id+"F0.wireOp",EDGE,"E1")])]}),"instanceName":"1"}),"instanceName":"1"}),"instanceName":"1"}),"instanceName":"1"}),"instanceName":"1"}),"instanceName":"1"}),"instanceName":"1"});
            var Q2245;
            Q2245=makeQuery(id+"F13.opPattern","COPY",BODY,{"derivedFrom":makeQuery(id+"F11.opPattern","COPY",BODY,{"derivedFrom":makeQuery(id+"F10.opPattern","COPY",BODY,{"derivedFrom":makeQuery(id+"F9.opPattern","COPY",BODY,{"derivedFrom":makeQuery(id+"F7.opPattern","COPY",BODY,{"derivedFrom":makeQuery(id+"F6.opPattern","COPY",BODY,{"derivedFrom":makeQuery(id+"F3.opPattern","COPY",BODY,{"derivedFrom":makeQuery(id+"F2.opPattern","COPY",BODY,{"derivedFrom":makeQuery(id+"F1.opRevolve","SWEPT_BODY",BODY,{"disambiguationData":[OSD([sQuery(id+"F0.wireOp",EDGE,"E1")])]}),"instanceName":"1"}),"instanceName":"1"}),"instanceName":"1"}),"instanceName":"1"}),"instanceName":"1"}),"instanceName":"1"}),"instanceName":"1"}),"instanceName":"1"});
            var Q2246;
            Q2246=makeQuery(id+"F13.opPattern","COPY",BODY,{"derivedFrom":makeQuery(id+"F11.opPattern","COPY",BODY,{"derivedFrom":makeQuery(id+"F10.opPattern","COPY",BODY,{"derivedFrom":makeQuery(id+"F9.opPattern","COPY",BODY,{"derivedFrom":makeQuery(id+"F7.opPattern","COPY",BODY,{"derivedFrom":makeQuery(id+"F6.opPattern","COPY",BODY,{"derivedFrom":makeQuery(id+"F4.opPattern","COPY",BODY,{"derivedFrom":makeQuery(id+"F1.opRevolve","SWEPT_BODY",BODY,{"disambiguationData":[OSD([sQuery(id+"F0.wireOp",EDGE,"E1")])]}),"instanceName":"1"}),"instanceName":"1"}),"instanceName":"1"}),"instanceName":"1"}),"instanceName":"1"}),"instanceName":"1"}),"instanceName":"1"});
            var Q2247;
            Q2247=makeQuery(id+"F13.opPattern","COPY",BODY,{"derivedFrom":makeQuery(id+"F11.opPattern","COPY",BODY,{"derivedFrom":makeQuery(id+"F10.opPattern","COPY",BODY,{"derivedFrom":makeQuery(id+"F9.opPattern","COPY",BODY,{"derivedFrom":makeQuery(id+"F7.opPattern","COPY",BODY,{"derivedFrom":makeQuery(id+"F6.opPattern","COPY",BODY,{"derivedFrom":makeQuery(id+"F4.opPattern","COPY",BODY,{"derivedFrom":makeQuery(id+"F2.opPattern","COPY",BODY,{"derivedFrom":makeQuery(id+"F1.opRevolve","SWEPT_BODY",BODY,{"disambiguationData":[OSD([sQuery(id+"F0.wireOp",EDGE,"E1")])]}),"instanceName":"1"}),"instanceName":"1"}),"instanceName":"1"}),"instanceName":"1"}),"instanceName":"1"}),"instanceName":"1"}),"instanceName":"1"}),"instanceName":"1"});
            var Q2248;
            Q2248=makeQuery(id+"F13.opPattern","COPY",BODY,{"derivedFrom":makeQuery(id+"F11.opPattern","COPY",BODY,{"derivedFrom":makeQuery(id+"F10.opPattern","COPY",BODY,{"derivedFrom":makeQuery(id+"F9.opPattern","COPY",BODY,{"derivedFrom":makeQuery(id+"F7.opPattern","COPY",BODY,{"derivedFrom":makeQuery(id+"F6.opPattern","COPY",BODY,{"derivedFrom":makeQuery(id+"F4.opPattern","COPY",BODY,{"derivedFrom":makeQuery(id+"F3.opPattern","COPY",BODY,{"derivedFrom":makeQuery(id+"F2.opPattern","COPY",BODY,{"derivedFrom":makeQuery(id+"F1.opRevolve","SWEPT_BODY",BODY,{"disambiguationData":[OSD([sQuery(id+"F0.wireOp",EDGE,"E1")])]}),"instanceName":"1"}),"instanceName":"1"}),"instanceName":"1"}),"instanceName":"1"}),"instanceName":"1"}),"instanceName":"1"}),"instanceName":"1"}),"instanceName":"1"}),"instanceName":"1"});
            var Q2249;
            Q2249=makeQuery(id+"F13.opPattern","COPY",BODY,{"derivedFrom":makeQuery(id+"F11.opPattern","COPY",BODY,{"derivedFrom":makeQuery(id+"F10.opPattern","COPY",BODY,{"derivedFrom":makeQuery(id+"F9.opPattern","COPY",BODY,{"derivedFrom":makeQuery(id+"F7.opPattern","COPY",BODY,{"derivedFrom":makeQuery(id+"F6.opPattern","COPY",BODY,{"derivedFrom":makeQuery(id+"F5.opPattern","COPY",BODY,{"derivedFrom":makeQuery(id+"F1.opRevolve","SWEPT_BODY",BODY,{"disambiguationData":[OSD([sQuery(id+"F0.wireOp",EDGE,"E1")])]}),"instanceName":"1"}),"instanceName":"1"}),"instanceName":"1"}),"instanceName":"1"}),"instanceName":"1"}),"instanceName":"1"}),"instanceName":"1"});
            var Q2250;
            Q2250=makeQuery(id+"F13.opPattern","COPY",BODY,{"derivedFrom":makeQuery(id+"F11.opPattern","COPY",BODY,{"derivedFrom":makeQuery(id+"F10.opPattern","COPY",BODY,{"derivedFrom":makeQuery(id+"F9.opPattern","COPY",BODY,{"derivedFrom":makeQuery(id+"F7.opPattern","COPY",BODY,{"derivedFrom":makeQuery(id+"F6.opPattern","COPY",BODY,{"derivedFrom":makeQuery(id+"F5.opPattern","COPY",BODY,{"derivedFrom":makeQuery(id+"F2.opPattern","COPY",BODY,{"derivedFrom":makeQuery(id+"F1.opRevolve","SWEPT_BODY",BODY,{"disambiguationData":[OSD([sQuery(id+"F0.wireOp",EDGE,"E1")])]}),"instanceName":"1"}),"instanceName":"1"}),"instanceName":"1"}),"instanceName":"1"}),"instanceName":"1"}),"instanceName":"1"}),"instanceName":"1"}),"instanceName":"1"});
            var Q2251;
            Q2251=makeQuery(id+"F13.opPattern","COPY",BODY,{"derivedFrom":makeQuery(id+"F11.opPattern","COPY",BODY,{"derivedFrom":makeQuery(id+"F10.opPattern","COPY",BODY,{"derivedFrom":makeQuery(id+"F9.opPattern","COPY",BODY,{"derivedFrom":makeQuery(id+"F7.opPattern","COPY",BODY,{"derivedFrom":makeQuery(id+"F6.opPattern","COPY",BODY,{"derivedFrom":makeQuery(id+"F5.opPattern","COPY",BODY,{"derivedFrom":makeQuery(id+"F3.opPattern","COPY",BODY,{"derivedFrom":makeQuery(id+"F2.opPattern","COPY",BODY,{"derivedFrom":makeQuery(id+"F1.opRevolve","SWEPT_BODY",BODY,{"disambiguationData":[OSD([sQuery(id+"F0.wireOp",EDGE,"E1")])]}),"instanceName":"1"}),"instanceName":"1"}),"instanceName":"1"}),"instanceName":"1"}),"instanceName":"1"}),"instanceName":"1"}),"instanceName":"1"}),"instanceName":"1"}),"instanceName":"1"});
            var Q2252;
            Q2252=makeQuery(id+"F13.opPattern","COPY",BODY,{"derivedFrom":makeQuery(id+"F11.opPattern","COPY",BODY,{"derivedFrom":makeQuery(id+"F10.opPattern","COPY",BODY,{"derivedFrom":makeQuery(id+"F9.opPattern","COPY",BODY,{"derivedFrom":makeQuery(id+"F7.opPattern","COPY",BODY,{"derivedFrom":makeQuery(id+"F6.opPattern","COPY",BODY,{"derivedFrom":makeQuery(id+"F5.opPattern","COPY",BODY,{"derivedFrom":makeQuery(id+"F4.opPattern","COPY",BODY,{"derivedFrom":makeQuery(id+"F1.opRevolve","SWEPT_BODY",BODY,{"disambiguationData":[OSD([sQuery(id+"F0.wireOp",EDGE,"E1")])]}),"instanceName":"1"}),"instanceName":"1"}),"instanceName":"1"}),"instanceName":"1"}),"instanceName":"1"}),"instanceName":"1"}),"instanceName":"1"}),"instanceName":"1"});
            var Q2253;
            Q2253=makeQuery(id+"F13.opPattern","COPY",BODY,{"derivedFrom":makeQuery(id+"F11.opPattern","COPY",BODY,{"derivedFrom":makeQuery(id+"F10.opPattern","COPY",BODY,{"derivedFrom":makeQuery(id+"F9.opPattern","COPY",BODY,{"derivedFrom":makeQuery(id+"F7.opPattern","COPY",BODY,{"derivedFrom":makeQuery(id+"F6.opPattern","COPY",BODY,{"derivedFrom":makeQuery(id+"F5.opPattern","COPY",BODY,{"derivedFrom":makeQuery(id+"F4.opPattern","COPY",BODY,{"derivedFrom":makeQuery(id+"F2.opPattern","COPY",BODY,{"derivedFrom":makeQuery(id+"F1.opRevolve","SWEPT_BODY",BODY,{"disambiguationData":[OSD([sQuery(id+"F0.wireOp",EDGE,"E1")])]}),"instanceName":"1"}),"instanceName":"1"}),"instanceName":"1"}),"instanceName":"1"}),"instanceName":"1"}),"instanceName":"1"}),"instanceName":"1"}),"instanceName":"1"}),"instanceName":"1"});
            var Q2254;
            Q2254=makeQuery(id+"F13.opPattern","COPY",BODY,{"derivedFrom":makeQuery(id+"F11.opPattern","COPY",BODY,{"derivedFrom":makeQuery(id+"F10.opPattern","COPY",BODY,{"derivedFrom":makeQuery(id+"F9.opPattern","COPY",BODY,{"derivedFrom":makeQuery(id+"F7.opPattern","COPY",BODY,{"derivedFrom":makeQuery(id+"F6.opPattern","COPY",BODY,{"derivedFrom":makeQuery(id+"F5.opPattern","COPY",BODY,{"derivedFrom":makeQuery(id+"F4.opPattern","COPY",BODY,{"derivedFrom":makeQuery(id+"F3.opPattern","COPY",BODY,{"derivedFrom":makeQuery(id+"F2.opPattern","COPY",BODY,{"derivedFrom":makeQuery(id+"F1.opRevolve","SWEPT_BODY",BODY,{"disambiguationData":[OSD([sQuery(id+"F0.wireOp",EDGE,"E1")])]}),"instanceName":"1"}),"instanceName":"1"}),"instanceName":"1"}),"instanceName":"1"}),"instanceName":"1"}),"instanceName":"1"}),"instanceName":"1"}),"instanceName":"1"}),"instanceName":"1"}),"instanceName":"1"});
            var Q2255;
            Q2255=makeQuery(id+"F13.opPattern","COPY",BODY,{"derivedFrom":makeQuery(id+"F11.opPattern","COPY",BODY,{"derivedFrom":makeQuery(id+"F10.opPattern","COPY",BODY,{"derivedFrom":makeQuery(id+"F9.opPattern","COPY",BODY,{"derivedFrom":makeQuery(id+"F8.opPattern","COPY",BODY,{"derivedFrom":makeQuery(id+"F1.opRevolve","SWEPT_BODY",BODY,{"disambiguationData":[OSD([sQuery(id+"F0.wireOp",EDGE,"E1")])]}),"instanceName":"1"}),"instanceName":"1"}),"instanceName":"1"}),"instanceName":"1"}),"instanceName":"1"});
            var Q2256;
            Q2256=makeQuery(id+"F13.opPattern","COPY",BODY,{"derivedFrom":makeQuery(id+"F11.opPattern","COPY",BODY,{"derivedFrom":makeQuery(id+"F10.opPattern","COPY",BODY,{"derivedFrom":makeQuery(id+"F9.opPattern","COPY",BODY,{"derivedFrom":makeQuery(id+"F8.opPattern","COPY",BODY,{"derivedFrom":makeQuery(id+"F2.opPattern","COPY",BODY,{"derivedFrom":makeQuery(id+"F1.opRevolve","SWEPT_BODY",BODY,{"disambiguationData":[OSD([sQuery(id+"F0.wireOp",EDGE,"E1")])]}),"instanceName":"1"}),"instanceName":"1"}),"instanceName":"1"}),"instanceName":"1"}),"instanceName":"1"}),"instanceName":"1"});
            var Q2257;
            Q2257=makeQuery(id+"F13.opPattern","COPY",BODY,{"derivedFrom":makeQuery(id+"F11.opPattern","COPY",BODY,{"derivedFrom":makeQuery(id+"F10.opPattern","COPY",BODY,{"derivedFrom":makeQuery(id+"F9.opPattern","COPY",BODY,{"derivedFrom":makeQuery(id+"F8.opPattern","COPY",BODY,{"derivedFrom":makeQuery(id+"F3.opPattern","COPY",BODY,{"derivedFrom":makeQuery(id+"F2.opPattern","COPY",BODY,{"derivedFrom":makeQuery(id+"F1.opRevolve","SWEPT_BODY",BODY,{"disambiguationData":[OSD([sQuery(id+"F0.wireOp",EDGE,"E1")])]}),"instanceName":"1"}),"instanceName":"1"}),"instanceName":"1"}),"instanceName":"1"}),"instanceName":"1"}),"instanceName":"1"}),"instanceName":"1"});
            var Q2258;
            Q2258=makeQuery(id+"F13.opPattern","COPY",BODY,{"derivedFrom":makeQuery(id+"F11.opPattern","COPY",BODY,{"derivedFrom":makeQuery(id+"F10.opPattern","COPY",BODY,{"derivedFrom":makeQuery(id+"F9.opPattern","COPY",BODY,{"derivedFrom":makeQuery(id+"F8.opPattern","COPY",BODY,{"derivedFrom":makeQuery(id+"F4.opPattern","COPY",BODY,{"derivedFrom":makeQuery(id+"F1.opRevolve","SWEPT_BODY",BODY,{"disambiguationData":[OSD([sQuery(id+"F0.wireOp",EDGE,"E1")])]}),"instanceName":"1"}),"instanceName":"1"}),"instanceName":"1"}),"instanceName":"1"}),"instanceName":"1"}),"instanceName":"1"});
            var Q2259;
            Q2259=makeQuery(id+"F13.opPattern","COPY",BODY,{"derivedFrom":makeQuery(id+"F11.opPattern","COPY",BODY,{"derivedFrom":makeQuery(id+"F10.opPattern","COPY",BODY,{"derivedFrom":makeQuery(id+"F9.opPattern","COPY",BODY,{"derivedFrom":makeQuery(id+"F8.opPattern","COPY",BODY,{"derivedFrom":makeQuery(id+"F4.opPattern","COPY",BODY,{"derivedFrom":makeQuery(id+"F2.opPattern","COPY",BODY,{"derivedFrom":makeQuery(id+"F1.opRevolve","SWEPT_BODY",BODY,{"disambiguationData":[OSD([sQuery(id+"F0.wireOp",EDGE,"E1")])]}),"instanceName":"1"}),"instanceName":"1"}),"instanceName":"1"}),"instanceName":"1"}),"instanceName":"1"}),"instanceName":"1"}),"instanceName":"1"});
            var Q2260;
            Q2260=makeQuery(id+"F13.opPattern","COPY",BODY,{"derivedFrom":makeQuery(id+"F11.opPattern","COPY",BODY,{"derivedFrom":makeQuery(id+"F10.opPattern","COPY",BODY,{"derivedFrom":makeQuery(id+"F9.opPattern","COPY",BODY,{"derivedFrom":makeQuery(id+"F8.opPattern","COPY",BODY,{"derivedFrom":makeQuery(id+"F4.opPattern","COPY",BODY,{"derivedFrom":makeQuery(id+"F3.opPattern","COPY",BODY,{"derivedFrom":makeQuery(id+"F2.opPattern","COPY",BODY,{"derivedFrom":makeQuery(id+"F1.opRevolve","SWEPT_BODY",BODY,{"disambiguationData":[OSD([sQuery(id+"F0.wireOp",EDGE,"E1")])]}),"instanceName":"1"}),"instanceName":"1"}),"instanceName":"1"}),"instanceName":"1"}),"instanceName":"1"}),"instanceName":"1"}),"instanceName":"1"}),"instanceName":"1"});
            var Q2261;
            Q2261=makeQuery(id+"F13.opPattern","COPY",BODY,{"derivedFrom":makeQuery(id+"F11.opPattern","COPY",BODY,{"derivedFrom":makeQuery(id+"F10.opPattern","COPY",BODY,{"derivedFrom":makeQuery(id+"F9.opPattern","COPY",BODY,{"derivedFrom":makeQuery(id+"F8.opPattern","COPY",BODY,{"derivedFrom":makeQuery(id+"F5.opPattern","COPY",BODY,{"derivedFrom":makeQuery(id+"F1.opRevolve","SWEPT_BODY",BODY,{"disambiguationData":[OSD([sQuery(id+"F0.wireOp",EDGE,"E1")])]}),"instanceName":"1"}),"instanceName":"1"}),"instanceName":"1"}),"instanceName":"1"}),"instanceName":"1"}),"instanceName":"1"});
            var Q2262;
            Q2262=makeQuery(id+"F13.opPattern","COPY",BODY,{"derivedFrom":makeQuery(id+"F11.opPattern","COPY",BODY,{"derivedFrom":makeQuery(id+"F10.opPattern","COPY",BODY,{"derivedFrom":makeQuery(id+"F9.opPattern","COPY",BODY,{"derivedFrom":makeQuery(id+"F8.opPattern","COPY",BODY,{"derivedFrom":makeQuery(id+"F5.opPattern","COPY",BODY,{"derivedFrom":makeQuery(id+"F2.opPattern","COPY",BODY,{"derivedFrom":makeQuery(id+"F1.opRevolve","SWEPT_BODY",BODY,{"disambiguationData":[OSD([sQuery(id+"F0.wireOp",EDGE,"E1")])]}),"instanceName":"1"}),"instanceName":"1"}),"instanceName":"1"}),"instanceName":"1"}),"instanceName":"1"}),"instanceName":"1"}),"instanceName":"1"});
            var Q2263;
            Q2263=makeQuery(id+"F13.opPattern","COPY",BODY,{"derivedFrom":makeQuery(id+"F11.opPattern","COPY",BODY,{"derivedFrom":makeQuery(id+"F10.opPattern","COPY",BODY,{"derivedFrom":makeQuery(id+"F9.opPattern","COPY",BODY,{"derivedFrom":makeQuery(id+"F8.opPattern","COPY",BODY,{"derivedFrom":makeQuery(id+"F5.opPattern","COPY",BODY,{"derivedFrom":makeQuery(id+"F3.opPattern","COPY",BODY,{"derivedFrom":makeQuery(id+"F2.opPattern","COPY",BODY,{"derivedFrom":makeQuery(id+"F1.opRevolve","SWEPT_BODY",BODY,{"disambiguationData":[OSD([sQuery(id+"F0.wireOp",EDGE,"E1")])]}),"instanceName":"1"}),"instanceName":"1"}),"instanceName":"1"}),"instanceName":"1"}),"instanceName":"1"}),"instanceName":"1"}),"instanceName":"1"}),"instanceName":"1"});
            var Q2264;
            Q2264=makeQuery(id+"F13.opPattern","COPY",BODY,{"derivedFrom":makeQuery(id+"F11.opPattern","COPY",BODY,{"derivedFrom":makeQuery(id+"F10.opPattern","COPY",BODY,{"derivedFrom":makeQuery(id+"F9.opPattern","COPY",BODY,{"derivedFrom":makeQuery(id+"F8.opPattern","COPY",BODY,{"derivedFrom":makeQuery(id+"F5.opPattern","COPY",BODY,{"derivedFrom":makeQuery(id+"F4.opPattern","COPY",BODY,{"derivedFrom":makeQuery(id+"F1.opRevolve","SWEPT_BODY",BODY,{"disambiguationData":[OSD([sQuery(id+"F0.wireOp",EDGE,"E1")])]}),"instanceName":"1"}),"instanceName":"1"}),"instanceName":"1"}),"instanceName":"1"}),"instanceName":"1"}),"instanceName":"1"}),"instanceName":"1"});
            var Q2265;
            Q2265=makeQuery(id+"F13.opPattern","COPY",BODY,{"derivedFrom":makeQuery(id+"F11.opPattern","COPY",BODY,{"derivedFrom":makeQuery(id+"F10.opPattern","COPY",BODY,{"derivedFrom":makeQuery(id+"F9.opPattern","COPY",BODY,{"derivedFrom":makeQuery(id+"F8.opPattern","COPY",BODY,{"derivedFrom":makeQuery(id+"F5.opPattern","COPY",BODY,{"derivedFrom":makeQuery(id+"F4.opPattern","COPY",BODY,{"derivedFrom":makeQuery(id+"F2.opPattern","COPY",BODY,{"derivedFrom":makeQuery(id+"F1.opRevolve","SWEPT_BODY",BODY,{"disambiguationData":[OSD([sQuery(id+"F0.wireOp",EDGE,"E1")])]}),"instanceName":"1"}),"instanceName":"1"}),"instanceName":"1"}),"instanceName":"1"}),"instanceName":"1"}),"instanceName":"1"}),"instanceName":"1"}),"instanceName":"1"});
            var Q2266;
            Q2266=makeQuery(id+"F13.opPattern","COPY",BODY,{"derivedFrom":makeQuery(id+"F11.opPattern","COPY",BODY,{"derivedFrom":makeQuery(id+"F10.opPattern","COPY",BODY,{"derivedFrom":makeQuery(id+"F9.opPattern","COPY",BODY,{"derivedFrom":makeQuery(id+"F8.opPattern","COPY",BODY,{"derivedFrom":makeQuery(id+"F5.opPattern","COPY",BODY,{"derivedFrom":makeQuery(id+"F4.opPattern","COPY",BODY,{"derivedFrom":makeQuery(id+"F3.opPattern","COPY",BODY,{"derivedFrom":makeQuery(id+"F2.opPattern","COPY",BODY,{"derivedFrom":makeQuery(id+"F1.opRevolve","SWEPT_BODY",BODY,{"disambiguationData":[OSD([sQuery(id+"F0.wireOp",EDGE,"E1")])]}),"instanceName":"1"}),"instanceName":"1"}),"instanceName":"1"}),"instanceName":"1"}),"instanceName":"1"}),"instanceName":"1"}),"instanceName":"1"}),"instanceName":"1"}),"instanceName":"1"});
            var Q2267;
            Q2267=makeQuery(id+"F13.opPattern","COPY",BODY,{"derivedFrom":makeQuery(id+"F11.opPattern","COPY",BODY,{"derivedFrom":makeQuery(id+"F10.opPattern","COPY",BODY,{"derivedFrom":makeQuery(id+"F9.opPattern","COPY",BODY,{"derivedFrom":makeQuery(id+"F8.opPattern","COPY",BODY,{"derivedFrom":makeQuery(id+"F6.opPattern","COPY",BODY,{"derivedFrom":makeQuery(id+"F1.opRevolve","SWEPT_BODY",BODY,{"disambiguationData":[OSD([sQuery(id+"F0.wireOp",EDGE,"E1")])]}),"instanceName":"1"}),"instanceName":"1"}),"instanceName":"1"}),"instanceName":"1"}),"instanceName":"1"}),"instanceName":"1"});
            var Q2268;
            Q2268=makeQuery(id+"F13.opPattern","COPY",BODY,{"derivedFrom":makeQuery(id+"F11.opPattern","COPY",BODY,{"derivedFrom":makeQuery(id+"F10.opPattern","COPY",BODY,{"derivedFrom":makeQuery(id+"F9.opPattern","COPY",BODY,{"derivedFrom":makeQuery(id+"F8.opPattern","COPY",BODY,{"derivedFrom":makeQuery(id+"F6.opPattern","COPY",BODY,{"derivedFrom":makeQuery(id+"F2.opPattern","COPY",BODY,{"derivedFrom":makeQuery(id+"F1.opRevolve","SWEPT_BODY",BODY,{"disambiguationData":[OSD([sQuery(id+"F0.wireOp",EDGE,"E1")])]}),"instanceName":"1"}),"instanceName":"1"}),"instanceName":"1"}),"instanceName":"1"}),"instanceName":"1"}),"instanceName":"1"}),"instanceName":"1"});
            var Q2269;
            Q2269=makeQuery(id+"F13.opPattern","COPY",BODY,{"derivedFrom":makeQuery(id+"F11.opPattern","COPY",BODY,{"derivedFrom":makeQuery(id+"F10.opPattern","COPY",BODY,{"derivedFrom":makeQuery(id+"F9.opPattern","COPY",BODY,{"derivedFrom":makeQuery(id+"F8.opPattern","COPY",BODY,{"derivedFrom":makeQuery(id+"F6.opPattern","COPY",BODY,{"derivedFrom":makeQuery(id+"F3.opPattern","COPY",BODY,{"derivedFrom":makeQuery(id+"F2.opPattern","COPY",BODY,{"derivedFrom":makeQuery(id+"F1.opRevolve","SWEPT_BODY",BODY,{"disambiguationData":[OSD([sQuery(id+"F0.wireOp",EDGE,"E1")])]}),"instanceName":"1"}),"instanceName":"1"}),"instanceName":"1"}),"instanceName":"1"}),"instanceName":"1"}),"instanceName":"1"}),"instanceName":"1"}),"instanceName":"1"});
            var Q2270;
            Q2270=makeQuery(id+"F13.opPattern","COPY",BODY,{"derivedFrom":makeQuery(id+"F11.opPattern","COPY",BODY,{"derivedFrom":makeQuery(id+"F10.opPattern","COPY",BODY,{"derivedFrom":makeQuery(id+"F9.opPattern","COPY",BODY,{"derivedFrom":makeQuery(id+"F8.opPattern","COPY",BODY,{"derivedFrom":makeQuery(id+"F6.opPattern","COPY",BODY,{"derivedFrom":makeQuery(id+"F4.opPattern","COPY",BODY,{"derivedFrom":makeQuery(id+"F1.opRevolve","SWEPT_BODY",BODY,{"disambiguationData":[OSD([sQuery(id+"F0.wireOp",EDGE,"E1")])]}),"instanceName":"1"}),"instanceName":"1"}),"instanceName":"1"}),"instanceName":"1"}),"instanceName":"1"}),"instanceName":"1"}),"instanceName":"1"});
            var Q2271;
            Q2271=makeQuery(id+"F13.opPattern","COPY",BODY,{"derivedFrom":makeQuery(id+"F11.opPattern","COPY",BODY,{"derivedFrom":makeQuery(id+"F10.opPattern","COPY",BODY,{"derivedFrom":makeQuery(id+"F9.opPattern","COPY",BODY,{"derivedFrom":makeQuery(id+"F8.opPattern","COPY",BODY,{"derivedFrom":makeQuery(id+"F6.opPattern","COPY",BODY,{"derivedFrom":makeQuery(id+"F4.opPattern","COPY",BODY,{"derivedFrom":makeQuery(id+"F2.opPattern","COPY",BODY,{"derivedFrom":makeQuery(id+"F1.opRevolve","SWEPT_BODY",BODY,{"disambiguationData":[OSD([sQuery(id+"F0.wireOp",EDGE,"E1")])]}),"instanceName":"1"}),"instanceName":"1"}),"instanceName":"1"}),"instanceName":"1"}),"instanceName":"1"}),"instanceName":"1"}),"instanceName":"1"}),"instanceName":"1"});
            var Q2272;
            Q2272=makeQuery(id+"F13.opPattern","COPY",BODY,{"derivedFrom":makeQuery(id+"F11.opPattern","COPY",BODY,{"derivedFrom":makeQuery(id+"F10.opPattern","COPY",BODY,{"derivedFrom":makeQuery(id+"F9.opPattern","COPY",BODY,{"derivedFrom":makeQuery(id+"F8.opPattern","COPY",BODY,{"derivedFrom":makeQuery(id+"F6.opPattern","COPY",BODY,{"derivedFrom":makeQuery(id+"F4.opPattern","COPY",BODY,{"derivedFrom":makeQuery(id+"F3.opPattern","COPY",BODY,{"derivedFrom":makeQuery(id+"F2.opPattern","COPY",BODY,{"derivedFrom":makeQuery(id+"F1.opRevolve","SWEPT_BODY",BODY,{"disambiguationData":[OSD([sQuery(id+"F0.wireOp",EDGE,"E1")])]}),"instanceName":"1"}),"instanceName":"1"}),"instanceName":"1"}),"instanceName":"1"}),"instanceName":"1"}),"instanceName":"1"}),"instanceName":"1"}),"instanceName":"1"}),"instanceName":"1"});
            var Q2273;
            Q2273=makeQuery(id+"F13.opPattern","COPY",BODY,{"derivedFrom":makeQuery(id+"F11.opPattern","COPY",BODY,{"derivedFrom":makeQuery(id+"F10.opPattern","COPY",BODY,{"derivedFrom":makeQuery(id+"F9.opPattern","COPY",BODY,{"derivedFrom":makeQuery(id+"F8.opPattern","COPY",BODY,{"derivedFrom":makeQuery(id+"F6.opPattern","COPY",BODY,{"derivedFrom":makeQuery(id+"F5.opPattern","COPY",BODY,{"derivedFrom":makeQuery(id+"F1.opRevolve","SWEPT_BODY",BODY,{"disambiguationData":[OSD([sQuery(id+"F0.wireOp",EDGE,"E1")])]}),"instanceName":"1"}),"instanceName":"1"}),"instanceName":"1"}),"instanceName":"1"}),"instanceName":"1"}),"instanceName":"1"}),"instanceName":"1"});
            var Q2274;
            Q2274=makeQuery(id+"F13.opPattern","COPY",BODY,{"derivedFrom":makeQuery(id+"F11.opPattern","COPY",BODY,{"derivedFrom":makeQuery(id+"F10.opPattern","COPY",BODY,{"derivedFrom":makeQuery(id+"F9.opPattern","COPY",BODY,{"derivedFrom":makeQuery(id+"F8.opPattern","COPY",BODY,{"derivedFrom":makeQuery(id+"F6.opPattern","COPY",BODY,{"derivedFrom":makeQuery(id+"F5.opPattern","COPY",BODY,{"derivedFrom":makeQuery(id+"F2.opPattern","COPY",BODY,{"derivedFrom":makeQuery(id+"F1.opRevolve","SWEPT_BODY",BODY,{"disambiguationData":[OSD([sQuery(id+"F0.wireOp",EDGE,"E1")])]}),"instanceName":"1"}),"instanceName":"1"}),"instanceName":"1"}),"instanceName":"1"}),"instanceName":"1"}),"instanceName":"1"}),"instanceName":"1"}),"instanceName":"1"});
            var Q2275;
            Q2275=makeQuery(id+"F13.opPattern","COPY",BODY,{"derivedFrom":makeQuery(id+"F11.opPattern","COPY",BODY,{"derivedFrom":makeQuery(id+"F10.opPattern","COPY",BODY,{"derivedFrom":makeQuery(id+"F9.opPattern","COPY",BODY,{"derivedFrom":makeQuery(id+"F8.opPattern","COPY",BODY,{"derivedFrom":makeQuery(id+"F6.opPattern","COPY",BODY,{"derivedFrom":makeQuery(id+"F5.opPattern","COPY",BODY,{"derivedFrom":makeQuery(id+"F3.opPattern","COPY",BODY,{"derivedFrom":makeQuery(id+"F2.opPattern","COPY",BODY,{"derivedFrom":makeQuery(id+"F1.opRevolve","SWEPT_BODY",BODY,{"disambiguationData":[OSD([sQuery(id+"F0.wireOp",EDGE,"E1")])]}),"instanceName":"1"}),"instanceName":"1"}),"instanceName":"1"}),"instanceName":"1"}),"instanceName":"1"}),"instanceName":"1"}),"instanceName":"1"}),"instanceName":"1"}),"instanceName":"1"});
            var Q2276;
            Q2276=makeQuery(id+"F13.opPattern","COPY",BODY,{"derivedFrom":makeQuery(id+"F11.opPattern","COPY",BODY,{"derivedFrom":makeQuery(id+"F10.opPattern","COPY",BODY,{"derivedFrom":makeQuery(id+"F9.opPattern","COPY",BODY,{"derivedFrom":makeQuery(id+"F8.opPattern","COPY",BODY,{"derivedFrom":makeQuery(id+"F6.opPattern","COPY",BODY,{"derivedFrom":makeQuery(id+"F5.opPattern","COPY",BODY,{"derivedFrom":makeQuery(id+"F4.opPattern","COPY",BODY,{"derivedFrom":makeQuery(id+"F1.opRevolve","SWEPT_BODY",BODY,{"disambiguationData":[OSD([sQuery(id+"F0.wireOp",EDGE,"E1")])]}),"instanceName":"1"}),"instanceName":"1"}),"instanceName":"1"}),"instanceName":"1"}),"instanceName":"1"}),"instanceName":"1"}),"instanceName":"1"}),"instanceName":"1"});
            var Q2277;
            Q2277=makeQuery(id+"F13.opPattern","COPY",BODY,{"derivedFrom":makeQuery(id+"F11.opPattern","COPY",BODY,{"derivedFrom":makeQuery(id+"F10.opPattern","COPY",BODY,{"derivedFrom":makeQuery(id+"F9.opPattern","COPY",BODY,{"derivedFrom":makeQuery(id+"F8.opPattern","COPY",BODY,{"derivedFrom":makeQuery(id+"F6.opPattern","COPY",BODY,{"derivedFrom":makeQuery(id+"F5.opPattern","COPY",BODY,{"derivedFrom":makeQuery(id+"F4.opPattern","COPY",BODY,{"derivedFrom":makeQuery(id+"F2.opPattern","COPY",BODY,{"derivedFrom":makeQuery(id+"F1.opRevolve","SWEPT_BODY",BODY,{"disambiguationData":[OSD([sQuery(id+"F0.wireOp",EDGE,"E1")])]}),"instanceName":"1"}),"instanceName":"1"}),"instanceName":"1"}),"instanceName":"1"}),"instanceName":"1"}),"instanceName":"1"}),"instanceName":"1"}),"instanceName":"1"}),"instanceName":"1"});
            var Q2278;
            Q2278=makeQuery(id+"F13.opPattern","COPY",BODY,{"derivedFrom":makeQuery(id+"F11.opPattern","COPY",BODY,{"derivedFrom":makeQuery(id+"F10.opPattern","COPY",BODY,{"derivedFrom":makeQuery(id+"F9.opPattern","COPY",BODY,{"derivedFrom":makeQuery(id+"F8.opPattern","COPY",BODY,{"derivedFrom":makeQuery(id+"F6.opPattern","COPY",BODY,{"derivedFrom":makeQuery(id+"F5.opPattern","COPY",BODY,{"derivedFrom":makeQuery(id+"F4.opPattern","COPY",BODY,{"derivedFrom":makeQuery(id+"F3.opPattern","COPY",BODY,{"derivedFrom":makeQuery(id+"F2.opPattern","COPY",BODY,{"derivedFrom":makeQuery(id+"F1.opRevolve","SWEPT_BODY",BODY,{"disambiguationData":[OSD([sQuery(id+"F0.wireOp",EDGE,"E1")])]}),"instanceName":"1"}),"instanceName":"1"}),"instanceName":"1"}),"instanceName":"1"}),"instanceName":"1"}),"instanceName":"1"}),"instanceName":"1"}),"instanceName":"1"}),"instanceName":"1"}),"instanceName":"1"});
            var Q2279;
            Q2279=makeQuery(id+"F13.opPattern","COPY",BODY,{"derivedFrom":makeQuery(id+"F11.opPattern","COPY",BODY,{"derivedFrom":makeQuery(id+"F10.opPattern","COPY",BODY,{"derivedFrom":makeQuery(id+"F9.opPattern","COPY",BODY,{"derivedFrom":makeQuery(id+"F8.opPattern","COPY",BODY,{"derivedFrom":makeQuery(id+"F7.opPattern","COPY",BODY,{"derivedFrom":makeQuery(id+"F1.opRevolve","SWEPT_BODY",BODY,{"disambiguationData":[OSD([sQuery(id+"F0.wireOp",EDGE,"E1")])]}),"instanceName":"1"}),"instanceName":"1"}),"instanceName":"1"}),"instanceName":"1"}),"instanceName":"1"}),"instanceName":"1"});
            var Q2280;
            Q2280=makeQuery(id+"F13.opPattern","COPY",BODY,{"derivedFrom":makeQuery(id+"F11.opPattern","COPY",BODY,{"derivedFrom":makeQuery(id+"F10.opPattern","COPY",BODY,{"derivedFrom":makeQuery(id+"F9.opPattern","COPY",BODY,{"derivedFrom":makeQuery(id+"F8.opPattern","COPY",BODY,{"derivedFrom":makeQuery(id+"F7.opPattern","COPY",BODY,{"derivedFrom":makeQuery(id+"F2.opPattern","COPY",BODY,{"derivedFrom":makeQuery(id+"F1.opRevolve","SWEPT_BODY",BODY,{"disambiguationData":[OSD([sQuery(id+"F0.wireOp",EDGE,"E1")])]}),"instanceName":"1"}),"instanceName":"1"}),"instanceName":"1"}),"instanceName":"1"}),"instanceName":"1"}),"instanceName":"1"}),"instanceName":"1"});
            var Q2281;
            Q2281=makeQuery(id+"F13.opPattern","COPY",BODY,{"derivedFrom":makeQuery(id+"F11.opPattern","COPY",BODY,{"derivedFrom":makeQuery(id+"F10.opPattern","COPY",BODY,{"derivedFrom":makeQuery(id+"F9.opPattern","COPY",BODY,{"derivedFrom":makeQuery(id+"F8.opPattern","COPY",BODY,{"derivedFrom":makeQuery(id+"F7.opPattern","COPY",BODY,{"derivedFrom":makeQuery(id+"F3.opPattern","COPY",BODY,{"derivedFrom":makeQuery(id+"F2.opPattern","COPY",BODY,{"derivedFrom":makeQuery(id+"F1.opRevolve","SWEPT_BODY",BODY,{"disambiguationData":[OSD([sQuery(id+"F0.wireOp",EDGE,"E1")])]}),"instanceName":"1"}),"instanceName":"1"}),"instanceName":"1"}),"instanceName":"1"}),"instanceName":"1"}),"instanceName":"1"}),"instanceName":"1"}),"instanceName":"1"});
            var Q2282;
            Q2282=makeQuery(id+"F13.opPattern","COPY",BODY,{"derivedFrom":makeQuery(id+"F11.opPattern","COPY",BODY,{"derivedFrom":makeQuery(id+"F10.opPattern","COPY",BODY,{"derivedFrom":makeQuery(id+"F9.opPattern","COPY",BODY,{"derivedFrom":makeQuery(id+"F8.opPattern","COPY",BODY,{"derivedFrom":makeQuery(id+"F7.opPattern","COPY",BODY,{"derivedFrom":makeQuery(id+"F4.opPattern","COPY",BODY,{"derivedFrom":makeQuery(id+"F1.opRevolve","SWEPT_BODY",BODY,{"disambiguationData":[OSD([sQuery(id+"F0.wireOp",EDGE,"E1")])]}),"instanceName":"1"}),"instanceName":"1"}),"instanceName":"1"}),"instanceName":"1"}),"instanceName":"1"}),"instanceName":"1"}),"instanceName":"1"});
            var Q2283;
            Q2283=makeQuery(id+"F13.opPattern","COPY",BODY,{"derivedFrom":makeQuery(id+"F11.opPattern","COPY",BODY,{"derivedFrom":makeQuery(id+"F10.opPattern","COPY",BODY,{"derivedFrom":makeQuery(id+"F9.opPattern","COPY",BODY,{"derivedFrom":makeQuery(id+"F8.opPattern","COPY",BODY,{"derivedFrom":makeQuery(id+"F7.opPattern","COPY",BODY,{"derivedFrom":makeQuery(id+"F4.opPattern","COPY",BODY,{"derivedFrom":makeQuery(id+"F2.opPattern","COPY",BODY,{"derivedFrom":makeQuery(id+"F1.opRevolve","SWEPT_BODY",BODY,{"disambiguationData":[OSD([sQuery(id+"F0.wireOp",EDGE,"E1")])]}),"instanceName":"1"}),"instanceName":"1"}),"instanceName":"1"}),"instanceName":"1"}),"instanceName":"1"}),"instanceName":"1"}),"instanceName":"1"}),"instanceName":"1"});
            var Q2284;
            Q2284=makeQuery(id+"F13.opPattern","COPY",BODY,{"derivedFrom":makeQuery(id+"F11.opPattern","COPY",BODY,{"derivedFrom":makeQuery(id+"F10.opPattern","COPY",BODY,{"derivedFrom":makeQuery(id+"F9.opPattern","COPY",BODY,{"derivedFrom":makeQuery(id+"F8.opPattern","COPY",BODY,{"derivedFrom":makeQuery(id+"F7.opPattern","COPY",BODY,{"derivedFrom":makeQuery(id+"F4.opPattern","COPY",BODY,{"derivedFrom":makeQuery(id+"F3.opPattern","COPY",BODY,{"derivedFrom":makeQuery(id+"F2.opPattern","COPY",BODY,{"derivedFrom":makeQuery(id+"F1.opRevolve","SWEPT_BODY",BODY,{"disambiguationData":[OSD([sQuery(id+"F0.wireOp",EDGE,"E1")])]}),"instanceName":"1"}),"instanceName":"1"}),"instanceName":"1"}),"instanceName":"1"}),"instanceName":"1"}),"instanceName":"1"}),"instanceName":"1"}),"instanceName":"1"}),"instanceName":"1"});
            var Q2285;
            Q2285=makeQuery(id+"F13.opPattern","COPY",BODY,{"derivedFrom":makeQuery(id+"F11.opPattern","COPY",BODY,{"derivedFrom":makeQuery(id+"F10.opPattern","COPY",BODY,{"derivedFrom":makeQuery(id+"F9.opPattern","COPY",BODY,{"derivedFrom":makeQuery(id+"F8.opPattern","COPY",BODY,{"derivedFrom":makeQuery(id+"F7.opPattern","COPY",BODY,{"derivedFrom":makeQuery(id+"F5.opPattern","COPY",BODY,{"derivedFrom":makeQuery(id+"F1.opRevolve","SWEPT_BODY",BODY,{"disambiguationData":[OSD([sQuery(id+"F0.wireOp",EDGE,"E1")])]}),"instanceName":"1"}),"instanceName":"1"}),"instanceName":"1"}),"instanceName":"1"}),"instanceName":"1"}),"instanceName":"1"}),"instanceName":"1"});
            var Q2286;
            Q2286=makeQuery(id+"F13.opPattern","COPY",BODY,{"derivedFrom":makeQuery(id+"F11.opPattern","COPY",BODY,{"derivedFrom":makeQuery(id+"F10.opPattern","COPY",BODY,{"derivedFrom":makeQuery(id+"F9.opPattern","COPY",BODY,{"derivedFrom":makeQuery(id+"F8.opPattern","COPY",BODY,{"derivedFrom":makeQuery(id+"F7.opPattern","COPY",BODY,{"derivedFrom":makeQuery(id+"F5.opPattern","COPY",BODY,{"derivedFrom":makeQuery(id+"F2.opPattern","COPY",BODY,{"derivedFrom":makeQuery(id+"F1.opRevolve","SWEPT_BODY",BODY,{"disambiguationData":[OSD([sQuery(id+"F0.wireOp",EDGE,"E1")])]}),"instanceName":"1"}),"instanceName":"1"}),"instanceName":"1"}),"instanceName":"1"}),"instanceName":"1"}),"instanceName":"1"}),"instanceName":"1"}),"instanceName":"1"});
            var Q2287;
            Q2287=makeQuery(id+"F13.opPattern","COPY",BODY,{"derivedFrom":makeQuery(id+"F11.opPattern","COPY",BODY,{"derivedFrom":makeQuery(id+"F10.opPattern","COPY",BODY,{"derivedFrom":makeQuery(id+"F9.opPattern","COPY",BODY,{"derivedFrom":makeQuery(id+"F8.opPattern","COPY",BODY,{"derivedFrom":makeQuery(id+"F7.opPattern","COPY",BODY,{"derivedFrom":makeQuery(id+"F5.opPattern","COPY",BODY,{"derivedFrom":makeQuery(id+"F3.opPattern","COPY",BODY,{"derivedFrom":makeQuery(id+"F2.opPattern","COPY",BODY,{"derivedFrom":makeQuery(id+"F1.opRevolve","SWEPT_BODY",BODY,{"disambiguationData":[OSD([sQuery(id+"F0.wireOp",EDGE,"E1")])]}),"instanceName":"1"}),"instanceName":"1"}),"instanceName":"1"}),"instanceName":"1"}),"instanceName":"1"}),"instanceName":"1"}),"instanceName":"1"}),"instanceName":"1"}),"instanceName":"1"});
            var Q2288;
            Q2288=makeQuery(id+"F13.opPattern","COPY",BODY,{"derivedFrom":makeQuery(id+"F11.opPattern","COPY",BODY,{"derivedFrom":makeQuery(id+"F10.opPattern","COPY",BODY,{"derivedFrom":makeQuery(id+"F9.opPattern","COPY",BODY,{"derivedFrom":makeQuery(id+"F8.opPattern","COPY",BODY,{"derivedFrom":makeQuery(id+"F7.opPattern","COPY",BODY,{"derivedFrom":makeQuery(id+"F5.opPattern","COPY",BODY,{"derivedFrom":makeQuery(id+"F4.opPattern","COPY",BODY,{"derivedFrom":makeQuery(id+"F1.opRevolve","SWEPT_BODY",BODY,{"disambiguationData":[OSD([sQuery(id+"F0.wireOp",EDGE,"E1")])]}),"instanceName":"1"}),"instanceName":"1"}),"instanceName":"1"}),"instanceName":"1"}),"instanceName":"1"}),"instanceName":"1"}),"instanceName":"1"}),"instanceName":"1"});
            var Q2289;
            Q2289=makeQuery(id+"F13.opPattern","COPY",BODY,{"derivedFrom":makeQuery(id+"F11.opPattern","COPY",BODY,{"derivedFrom":makeQuery(id+"F10.opPattern","COPY",BODY,{"derivedFrom":makeQuery(id+"F9.opPattern","COPY",BODY,{"derivedFrom":makeQuery(id+"F8.opPattern","COPY",BODY,{"derivedFrom":makeQuery(id+"F7.opPattern","COPY",BODY,{"derivedFrom":makeQuery(id+"F5.opPattern","COPY",BODY,{"derivedFrom":makeQuery(id+"F4.opPattern","COPY",BODY,{"derivedFrom":makeQuery(id+"F2.opPattern","COPY",BODY,{"derivedFrom":makeQuery(id+"F1.opRevolve","SWEPT_BODY",BODY,{"disambiguationData":[OSD([sQuery(id+"F0.wireOp",EDGE,"E1")])]}),"instanceName":"1"}),"instanceName":"1"}),"instanceName":"1"}),"instanceName":"1"}),"instanceName":"1"}),"instanceName":"1"}),"instanceName":"1"}),"instanceName":"1"}),"instanceName":"1"});
            var Q2290;
            Q2290=makeQuery(id+"F13.opPattern","COPY",BODY,{"derivedFrom":makeQuery(id+"F11.opPattern","COPY",BODY,{"derivedFrom":makeQuery(id+"F10.opPattern","COPY",BODY,{"derivedFrom":makeQuery(id+"F9.opPattern","COPY",BODY,{"derivedFrom":makeQuery(id+"F8.opPattern","COPY",BODY,{"derivedFrom":makeQuery(id+"F7.opPattern","COPY",BODY,{"derivedFrom":makeQuery(id+"F5.opPattern","COPY",BODY,{"derivedFrom":makeQuery(id+"F4.opPattern","COPY",BODY,{"derivedFrom":makeQuery(id+"F3.opPattern","COPY",BODY,{"derivedFrom":makeQuery(id+"F2.opPattern","COPY",BODY,{"derivedFrom":makeQuery(id+"F1.opRevolve","SWEPT_BODY",BODY,{"disambiguationData":[OSD([sQuery(id+"F0.wireOp",EDGE,"E1")])]}),"instanceName":"1"}),"instanceName":"1"}),"instanceName":"1"}),"instanceName":"1"}),"instanceName":"1"}),"instanceName":"1"}),"instanceName":"1"}),"instanceName":"1"}),"instanceName":"1"}),"instanceName":"1"});
            var Q2291;
            Q2291=makeQuery(id+"F13.opPattern","COPY",BODY,{"derivedFrom":makeQuery(id+"F11.opPattern","COPY",BODY,{"derivedFrom":makeQuery(id+"F10.opPattern","COPY",BODY,{"derivedFrom":makeQuery(id+"F9.opPattern","COPY",BODY,{"derivedFrom":makeQuery(id+"F8.opPattern","COPY",BODY,{"derivedFrom":makeQuery(id+"F7.opPattern","COPY",BODY,{"derivedFrom":makeQuery(id+"F6.opPattern","COPY",BODY,{"derivedFrom":makeQuery(id+"F1.opRevolve","SWEPT_BODY",BODY,{"disambiguationData":[OSD([sQuery(id+"F0.wireOp",EDGE,"E1")])]}),"instanceName":"1"}),"instanceName":"1"}),"instanceName":"1"}),"instanceName":"1"}),"instanceName":"1"}),"instanceName":"1"}),"instanceName":"1"});
            var Q2292;
            Q2292=makeQuery(id+"F13.opPattern","COPY",BODY,{"derivedFrom":makeQuery(id+"F11.opPattern","COPY",BODY,{"derivedFrom":makeQuery(id+"F10.opPattern","COPY",BODY,{"derivedFrom":makeQuery(id+"F9.opPattern","COPY",BODY,{"derivedFrom":makeQuery(id+"F8.opPattern","COPY",BODY,{"derivedFrom":makeQuery(id+"F7.opPattern","COPY",BODY,{"derivedFrom":makeQuery(id+"F6.opPattern","COPY",BODY,{"derivedFrom":makeQuery(id+"F2.opPattern","COPY",BODY,{"derivedFrom":makeQuery(id+"F1.opRevolve","SWEPT_BODY",BODY,{"disambiguationData":[OSD([sQuery(id+"F0.wireOp",EDGE,"E1")])]}),"instanceName":"1"}),"instanceName":"1"}),"instanceName":"1"}),"instanceName":"1"}),"instanceName":"1"}),"instanceName":"1"}),"instanceName":"1"}),"instanceName":"1"});
            var Q2293;
            Q2293=makeQuery(id+"F13.opPattern","COPY",BODY,{"derivedFrom":makeQuery(id+"F11.opPattern","COPY",BODY,{"derivedFrom":makeQuery(id+"F10.opPattern","COPY",BODY,{"derivedFrom":makeQuery(id+"F9.opPattern","COPY",BODY,{"derivedFrom":makeQuery(id+"F8.opPattern","COPY",BODY,{"derivedFrom":makeQuery(id+"F7.opPattern","COPY",BODY,{"derivedFrom":makeQuery(id+"F6.opPattern","COPY",BODY,{"derivedFrom":makeQuery(id+"F3.opPattern","COPY",BODY,{"derivedFrom":makeQuery(id+"F2.opPattern","COPY",BODY,{"derivedFrom":makeQuery(id+"F1.opRevolve","SWEPT_BODY",BODY,{"disambiguationData":[OSD([sQuery(id+"F0.wireOp",EDGE,"E1")])]}),"instanceName":"1"}),"instanceName":"1"}),"instanceName":"1"}),"instanceName":"1"}),"instanceName":"1"}),"instanceName":"1"}),"instanceName":"1"}),"instanceName":"1"}),"instanceName":"1"});
            var Q2294;
            Q2294=makeQuery(id+"F13.opPattern","COPY",BODY,{"derivedFrom":makeQuery(id+"F11.opPattern","COPY",BODY,{"derivedFrom":makeQuery(id+"F10.opPattern","COPY",BODY,{"derivedFrom":makeQuery(id+"F9.opPattern","COPY",BODY,{"derivedFrom":makeQuery(id+"F8.opPattern","COPY",BODY,{"derivedFrom":makeQuery(id+"F7.opPattern","COPY",BODY,{"derivedFrom":makeQuery(id+"F6.opPattern","COPY",BODY,{"derivedFrom":makeQuery(id+"F4.opPattern","COPY",BODY,{"derivedFrom":makeQuery(id+"F1.opRevolve","SWEPT_BODY",BODY,{"disambiguationData":[OSD([sQuery(id+"F0.wireOp",EDGE,"E1")])]}),"instanceName":"1"}),"instanceName":"1"}),"instanceName":"1"}),"instanceName":"1"}),"instanceName":"1"}),"instanceName":"1"}),"instanceName":"1"}),"instanceName":"1"});
            var Q2295;
            Q2295=makeQuery(id+"F13.opPattern","COPY",BODY,{"derivedFrom":makeQuery(id+"F11.opPattern","COPY",BODY,{"derivedFrom":makeQuery(id+"F10.opPattern","COPY",BODY,{"derivedFrom":makeQuery(id+"F9.opPattern","COPY",BODY,{"derivedFrom":makeQuery(id+"F8.opPattern","COPY",BODY,{"derivedFrom":makeQuery(id+"F7.opPattern","COPY",BODY,{"derivedFrom":makeQuery(id+"F6.opPattern","COPY",BODY,{"derivedFrom":makeQuery(id+"F4.opPattern","COPY",BODY,{"derivedFrom":makeQuery(id+"F2.opPattern","COPY",BODY,{"derivedFrom":makeQuery(id+"F1.opRevolve","SWEPT_BODY",BODY,{"disambiguationData":[OSD([sQuery(id+"F0.wireOp",EDGE,"E1")])]}),"instanceName":"1"}),"instanceName":"1"}),"instanceName":"1"}),"instanceName":"1"}),"instanceName":"1"}),"instanceName":"1"}),"instanceName":"1"}),"instanceName":"1"}),"instanceName":"1"});
            var Q2296;
            Q2296=makeQuery(id+"F13.opPattern","COPY",BODY,{"derivedFrom":makeQuery(id+"F11.opPattern","COPY",BODY,{"derivedFrom":makeQuery(id+"F10.opPattern","COPY",BODY,{"derivedFrom":makeQuery(id+"F9.opPattern","COPY",BODY,{"derivedFrom":makeQuery(id+"F8.opPattern","COPY",BODY,{"derivedFrom":makeQuery(id+"F7.opPattern","COPY",BODY,{"derivedFrom":makeQuery(id+"F6.opPattern","COPY",BODY,{"derivedFrom":makeQuery(id+"F4.opPattern","COPY",BODY,{"derivedFrom":makeQuery(id+"F3.opPattern","COPY",BODY,{"derivedFrom":makeQuery(id+"F2.opPattern","COPY",BODY,{"derivedFrom":makeQuery(id+"F1.opRevolve","SWEPT_BODY",BODY,{"disambiguationData":[OSD([sQuery(id+"F0.wireOp",EDGE,"E1")])]}),"instanceName":"1"}),"instanceName":"1"}),"instanceName":"1"}),"instanceName":"1"}),"instanceName":"1"}),"instanceName":"1"}),"instanceName":"1"}),"instanceName":"1"}),"instanceName":"1"}),"instanceName":"1"});
            var Q2297;
            Q2297=makeQuery(id+"F13.opPattern","COPY",BODY,{"derivedFrom":makeQuery(id+"F11.opPattern","COPY",BODY,{"derivedFrom":makeQuery(id+"F10.opPattern","COPY",BODY,{"derivedFrom":makeQuery(id+"F9.opPattern","COPY",BODY,{"derivedFrom":makeQuery(id+"F8.opPattern","COPY",BODY,{"derivedFrom":makeQuery(id+"F7.opPattern","COPY",BODY,{"derivedFrom":makeQuery(id+"F6.opPattern","COPY",BODY,{"derivedFrom":makeQuery(id+"F5.opPattern","COPY",BODY,{"derivedFrom":makeQuery(id+"F1.opRevolve","SWEPT_BODY",BODY,{"disambiguationData":[OSD([sQuery(id+"F0.wireOp",EDGE,"E1")])]}),"instanceName":"1"}),"instanceName":"1"}),"instanceName":"1"}),"instanceName":"1"}),"instanceName":"1"}),"instanceName":"1"}),"instanceName":"1"}),"instanceName":"1"});
            var Q2298;
            Q2298=makeQuery(id+"F13.opPattern","COPY",BODY,{"derivedFrom":makeQuery(id+"F11.opPattern","COPY",BODY,{"derivedFrom":makeQuery(id+"F10.opPattern","COPY",BODY,{"derivedFrom":makeQuery(id+"F9.opPattern","COPY",BODY,{"derivedFrom":makeQuery(id+"F8.opPattern","COPY",BODY,{"derivedFrom":makeQuery(id+"F7.opPattern","COPY",BODY,{"derivedFrom":makeQuery(id+"F6.opPattern","COPY",BODY,{"derivedFrom":makeQuery(id+"F5.opPattern","COPY",BODY,{"derivedFrom":makeQuery(id+"F2.opPattern","COPY",BODY,{"derivedFrom":makeQuery(id+"F1.opRevolve","SWEPT_BODY",BODY,{"disambiguationData":[OSD([sQuery(id+"F0.wireOp",EDGE,"E1")])]}),"instanceName":"1"}),"instanceName":"1"}),"instanceName":"1"}),"instanceName":"1"}),"instanceName":"1"}),"instanceName":"1"}),"instanceName":"1"}),"instanceName":"1"}),"instanceName":"1"});
            var Q2299;
            Q2299=makeQuery(id+"F13.opPattern","COPY",BODY,{"derivedFrom":makeQuery(id+"F11.opPattern","COPY",BODY,{"derivedFrom":makeQuery(id+"F10.opPattern","COPY",BODY,{"derivedFrom":makeQuery(id+"F9.opPattern","COPY",BODY,{"derivedFrom":makeQuery(id+"F8.opPattern","COPY",BODY,{"derivedFrom":makeQuery(id+"F7.opPattern","COPY",BODY,{"derivedFrom":makeQuery(id+"F6.opPattern","COPY",BODY,{"derivedFrom":makeQuery(id+"F5.opPattern","COPY",BODY,{"derivedFrom":makeQuery(id+"F3.opPattern","COPY",BODY,{"derivedFrom":makeQuery(id+"F2.opPattern","COPY",BODY,{"derivedFrom":makeQuery(id+"F1.opRevolve","SWEPT_BODY",BODY,{"disambiguationData":[OSD([sQuery(id+"F0.wireOp",EDGE,"E1")])]}),"instanceName":"1"}),"instanceName":"1"}),"instanceName":"1"}),"instanceName":"1"}),"instanceName":"1"}),"instanceName":"1"}),"instanceName":"1"}),"instanceName":"1"}),"instanceName":"1"}),"instanceName":"1"});
            var Q2300;
            Q2300=makeQuery(id+"F13.opPattern","COPY",BODY,{"derivedFrom":makeQuery(id+"F11.opPattern","COPY",BODY,{"derivedFrom":makeQuery(id+"F10.opPattern","COPY",BODY,{"derivedFrom":makeQuery(id+"F9.opPattern","COPY",BODY,{"derivedFrom":makeQuery(id+"F8.opPattern","COPY",BODY,{"derivedFrom":makeQuery(id+"F7.opPattern","COPY",BODY,{"derivedFrom":makeQuery(id+"F6.opPattern","COPY",BODY,{"derivedFrom":makeQuery(id+"F5.opPattern","COPY",BODY,{"derivedFrom":makeQuery(id+"F4.opPattern","COPY",BODY,{"derivedFrom":makeQuery(id+"F1.opRevolve","SWEPT_BODY",BODY,{"disambiguationData":[OSD([sQuery(id+"F0.wireOp",EDGE,"E1")])]}),"instanceName":"1"}),"instanceName":"1"}),"instanceName":"1"}),"instanceName":"1"}),"instanceName":"1"}),"instanceName":"1"}),"instanceName":"1"}),"instanceName":"1"}),"instanceName":"1"});
            var Q2301;
            Q2301=makeQuery(id+"F13.opPattern","COPY",BODY,{"derivedFrom":makeQuery(id+"F11.opPattern","COPY",BODY,{"derivedFrom":makeQuery(id+"F10.opPattern","COPY",BODY,{"derivedFrom":makeQuery(id+"F9.opPattern","COPY",BODY,{"derivedFrom":makeQuery(id+"F8.opPattern","COPY",BODY,{"derivedFrom":makeQuery(id+"F7.opPattern","COPY",BODY,{"derivedFrom":makeQuery(id+"F6.opPattern","COPY",BODY,{"derivedFrom":makeQuery(id+"F5.opPattern","COPY",BODY,{"derivedFrom":makeQuery(id+"F4.opPattern","COPY",BODY,{"derivedFrom":makeQuery(id+"F2.opPattern","COPY",BODY,{"derivedFrom":makeQuery(id+"F1.opRevolve","SWEPT_BODY",BODY,{"disambiguationData":[OSD([sQuery(id+"F0.wireOp",EDGE,"E1")])]}),"instanceName":"1"}),"instanceName":"1"}),"instanceName":"1"}),"instanceName":"1"}),"instanceName":"1"}),"instanceName":"1"}),"instanceName":"1"}),"instanceName":"1"}),"instanceName":"1"}),"instanceName":"1"});
            var Q2302;
            Q2302=makeQuery(id+"F13.opPattern","COPY",BODY,{"derivedFrom":makeQuery(id+"F11.opPattern","COPY",BODY,{"derivedFrom":makeQuery(id+"F10.opPattern","COPY",BODY,{"derivedFrom":makeQuery(id+"F9.opPattern","COPY",BODY,{"derivedFrom":makeQuery(id+"F8.opPattern","COPY",BODY,{"derivedFrom":makeQuery(id+"F7.opPattern","COPY",BODY,{"derivedFrom":makeQuery(id+"F6.opPattern","COPY",BODY,{"derivedFrom":makeQuery(id+"F5.opPattern","COPY",BODY,{"derivedFrom":makeQuery(id+"F4.opPattern","COPY",BODY,{"derivedFrom":makeQuery(id+"F3.opPattern","COPY",BODY,{"derivedFrom":makeQuery(id+"F2.opPattern","COPY",BODY,{"derivedFrom":makeQuery(id+"F1.opRevolve","SWEPT_BODY",BODY,{"disambiguationData":[OSD([sQuery(id+"F0.wireOp",EDGE,"E1")])]}),"instanceName":"1"}),"instanceName":"1"}),"instanceName":"1"}),"instanceName":"1"}),"instanceName":"1"}),"instanceName":"1"}),"instanceName":"1"}),"instanceName":"1"}),"instanceName":"1"}),"instanceName":"1"}),"instanceName":"1"});
            var Q2303;
            Q2303=makeQuery(id+"F13.opPattern","COPY",BODY,{"derivedFrom":makeQuery(id+"F12.opPattern","COPY",BODY,{"derivedFrom":makeQuery(id+"F1.opRevolve","SWEPT_BODY",BODY,{"disambiguationData":[OSD([sQuery(id+"F0.wireOp",EDGE,"E1")])]}),"instanceName":"1"}),"instanceName":"1"});
            var Q2304;
            Q2304=makeQuery(id+"F13.opPattern","COPY",BODY,{"derivedFrom":makeQuery(id+"F12.opPattern","COPY",BODY,{"derivedFrom":makeQuery(id+"F2.opPattern","COPY",BODY,{"derivedFrom":makeQuery(id+"F1.opRevolve","SWEPT_BODY",BODY,{"disambiguationData":[OSD([sQuery(id+"F0.wireOp",EDGE,"E1")])]}),"instanceName":"1"}),"instanceName":"1"}),"instanceName":"1"});
            var Q2305;
            Q2305=makeQuery(id+"F13.opPattern","COPY",BODY,{"derivedFrom":makeQuery(id+"F12.opPattern","COPY",BODY,{"derivedFrom":makeQuery(id+"F3.opPattern","COPY",BODY,{"derivedFrom":makeQuery(id+"F2.opPattern","COPY",BODY,{"derivedFrom":makeQuery(id+"F1.opRevolve","SWEPT_BODY",BODY,{"disambiguationData":[OSD([sQuery(id+"F0.wireOp",EDGE,"E1")])]}),"instanceName":"1"}),"instanceName":"1"}),"instanceName":"1"}),"instanceName":"1"});
            var Q2306;
            Q2306=makeQuery(id+"F13.opPattern","COPY",BODY,{"derivedFrom":makeQuery(id+"F12.opPattern","COPY",BODY,{"derivedFrom":makeQuery(id+"F4.opPattern","COPY",BODY,{"derivedFrom":makeQuery(id+"F1.opRevolve","SWEPT_BODY",BODY,{"disambiguationData":[OSD([sQuery(id+"F0.wireOp",EDGE,"E1")])]}),"instanceName":"1"}),"instanceName":"1"}),"instanceName":"1"});
            var Q2307;
            Q2307=makeQuery(id+"F13.opPattern","COPY",BODY,{"derivedFrom":makeQuery(id+"F12.opPattern","COPY",BODY,{"derivedFrom":makeQuery(id+"F4.opPattern","COPY",BODY,{"derivedFrom":makeQuery(id+"F2.opPattern","COPY",BODY,{"derivedFrom":makeQuery(id+"F1.opRevolve","SWEPT_BODY",BODY,{"disambiguationData":[OSD([sQuery(id+"F0.wireOp",EDGE,"E1")])]}),"instanceName":"1"}),"instanceName":"1"}),"instanceName":"1"}),"instanceName":"1"});
            var Q2308;
            Q2308=makeQuery(id+"F13.opPattern","COPY",BODY,{"derivedFrom":makeQuery(id+"F12.opPattern","COPY",BODY,{"derivedFrom":makeQuery(id+"F4.opPattern","COPY",BODY,{"derivedFrom":makeQuery(id+"F3.opPattern","COPY",BODY,{"derivedFrom":makeQuery(id+"F2.opPattern","COPY",BODY,{"derivedFrom":makeQuery(id+"F1.opRevolve","SWEPT_BODY",BODY,{"disambiguationData":[OSD([sQuery(id+"F0.wireOp",EDGE,"E1")])]}),"instanceName":"1"}),"instanceName":"1"}),"instanceName":"1"}),"instanceName":"1"}),"instanceName":"1"});
            var Q2309;
            Q2309=makeQuery(id+"F13.opPattern","COPY",BODY,{"derivedFrom":makeQuery(id+"F12.opPattern","COPY",BODY,{"derivedFrom":makeQuery(id+"F5.opPattern","COPY",BODY,{"derivedFrom":makeQuery(id+"F1.opRevolve","SWEPT_BODY",BODY,{"disambiguationData":[OSD([sQuery(id+"F0.wireOp",EDGE,"E1")])]}),"instanceName":"1"}),"instanceName":"1"}),"instanceName":"1"});
            var Q2310;
            Q2310=makeQuery(id+"F13.opPattern","COPY",BODY,{"derivedFrom":makeQuery(id+"F12.opPattern","COPY",BODY,{"derivedFrom":makeQuery(id+"F5.opPattern","COPY",BODY,{"derivedFrom":makeQuery(id+"F2.opPattern","COPY",BODY,{"derivedFrom":makeQuery(id+"F1.opRevolve","SWEPT_BODY",BODY,{"disambiguationData":[OSD([sQuery(id+"F0.wireOp",EDGE,"E1")])]}),"instanceName":"1"}),"instanceName":"1"}),"instanceName":"1"}),"instanceName":"1"});
            var Q2311;
            Q2311=makeQuery(id+"F13.opPattern","COPY",BODY,{"derivedFrom":makeQuery(id+"F12.opPattern","COPY",BODY,{"derivedFrom":makeQuery(id+"F5.opPattern","COPY",BODY,{"derivedFrom":makeQuery(id+"F3.opPattern","COPY",BODY,{"derivedFrom":makeQuery(id+"F2.opPattern","COPY",BODY,{"derivedFrom":makeQuery(id+"F1.opRevolve","SWEPT_BODY",BODY,{"disambiguationData":[OSD([sQuery(id+"F0.wireOp",EDGE,"E1")])]}),"instanceName":"1"}),"instanceName":"1"}),"instanceName":"1"}),"instanceName":"1"}),"instanceName":"1"});
            var Q2312;
            Q2312=makeQuery(id+"F13.opPattern","COPY",BODY,{"derivedFrom":makeQuery(id+"F12.opPattern","COPY",BODY,{"derivedFrom":makeQuery(id+"F5.opPattern","COPY",BODY,{"derivedFrom":makeQuery(id+"F4.opPattern","COPY",BODY,{"derivedFrom":makeQuery(id+"F1.opRevolve","SWEPT_BODY",BODY,{"disambiguationData":[OSD([sQuery(id+"F0.wireOp",EDGE,"E1")])]}),"instanceName":"1"}),"instanceName":"1"}),"instanceName":"1"}),"instanceName":"1"});
            var Q2313;
            Q2313=makeQuery(id+"F13.opPattern","COPY",BODY,{"derivedFrom":makeQuery(id+"F12.opPattern","COPY",BODY,{"derivedFrom":makeQuery(id+"F5.opPattern","COPY",BODY,{"derivedFrom":makeQuery(id+"F4.opPattern","COPY",BODY,{"derivedFrom":makeQuery(id+"F2.opPattern","COPY",BODY,{"derivedFrom":makeQuery(id+"F1.opRevolve","SWEPT_BODY",BODY,{"disambiguationData":[OSD([sQuery(id+"F0.wireOp",EDGE,"E1")])]}),"instanceName":"1"}),"instanceName":"1"}),"instanceName":"1"}),"instanceName":"1"}),"instanceName":"1"});
            var Q2314;
            Q2314=makeQuery(id+"F13.opPattern","COPY",BODY,{"derivedFrom":makeQuery(id+"F12.opPattern","COPY",BODY,{"derivedFrom":makeQuery(id+"F5.opPattern","COPY",BODY,{"derivedFrom":makeQuery(id+"F4.opPattern","COPY",BODY,{"derivedFrom":makeQuery(id+"F3.opPattern","COPY",BODY,{"derivedFrom":makeQuery(id+"F2.opPattern","COPY",BODY,{"derivedFrom":makeQuery(id+"F1.opRevolve","SWEPT_BODY",BODY,{"disambiguationData":[OSD([sQuery(id+"F0.wireOp",EDGE,"E1")])]}),"instanceName":"1"}),"instanceName":"1"}),"instanceName":"1"}),"instanceName":"1"}),"instanceName":"1"}),"instanceName":"1"});
            var Q2315;
            Q2315=makeQuery(id+"F13.opPattern","COPY",BODY,{"derivedFrom":makeQuery(id+"F12.opPattern","COPY",BODY,{"derivedFrom":makeQuery(id+"F6.opPattern","COPY",BODY,{"derivedFrom":makeQuery(id+"F1.opRevolve","SWEPT_BODY",BODY,{"disambiguationData":[OSD([sQuery(id+"F0.wireOp",EDGE,"E1")])]}),"instanceName":"1"}),"instanceName":"1"}),"instanceName":"1"});
            var Q2316;
            Q2316=makeQuery(id+"F13.opPattern","COPY",BODY,{"derivedFrom":makeQuery(id+"F12.opPattern","COPY",BODY,{"derivedFrom":makeQuery(id+"F6.opPattern","COPY",BODY,{"derivedFrom":makeQuery(id+"F2.opPattern","COPY",BODY,{"derivedFrom":makeQuery(id+"F1.opRevolve","SWEPT_BODY",BODY,{"disambiguationData":[OSD([sQuery(id+"F0.wireOp",EDGE,"E1")])]}),"instanceName":"1"}),"instanceName":"1"}),"instanceName":"1"}),"instanceName":"1"});
            var Q2317;
            Q2317=makeQuery(id+"F13.opPattern","COPY",BODY,{"derivedFrom":makeQuery(id+"F12.opPattern","COPY",BODY,{"derivedFrom":makeQuery(id+"F6.opPattern","COPY",BODY,{"derivedFrom":makeQuery(id+"F3.opPattern","COPY",BODY,{"derivedFrom":makeQuery(id+"F2.opPattern","COPY",BODY,{"derivedFrom":makeQuery(id+"F1.opRevolve","SWEPT_BODY",BODY,{"disambiguationData":[OSD([sQuery(id+"F0.wireOp",EDGE,"E1")])]}),"instanceName":"1"}),"instanceName":"1"}),"instanceName":"1"}),"instanceName":"1"}),"instanceName":"1"});
            var Q2318;
            Q2318=makeQuery(id+"F13.opPattern","COPY",BODY,{"derivedFrom":makeQuery(id+"F12.opPattern","COPY",BODY,{"derivedFrom":makeQuery(id+"F6.opPattern","COPY",BODY,{"derivedFrom":makeQuery(id+"F4.opPattern","COPY",BODY,{"derivedFrom":makeQuery(id+"F1.opRevolve","SWEPT_BODY",BODY,{"disambiguationData":[OSD([sQuery(id+"F0.wireOp",EDGE,"E1")])]}),"instanceName":"1"}),"instanceName":"1"}),"instanceName":"1"}),"instanceName":"1"});
            var Q2319;
            Q2319=makeQuery(id+"F13.opPattern","COPY",BODY,{"derivedFrom":makeQuery(id+"F12.opPattern","COPY",BODY,{"derivedFrom":makeQuery(id+"F6.opPattern","COPY",BODY,{"derivedFrom":makeQuery(id+"F4.opPattern","COPY",BODY,{"derivedFrom":makeQuery(id+"F2.opPattern","COPY",BODY,{"derivedFrom":makeQuery(id+"F1.opRevolve","SWEPT_BODY",BODY,{"disambiguationData":[OSD([sQuery(id+"F0.wireOp",EDGE,"E1")])]}),"instanceName":"1"}),"instanceName":"1"}),"instanceName":"1"}),"instanceName":"1"}),"instanceName":"1"});
            var Q2320;
            Q2320=makeQuery(id+"F13.opPattern","COPY",BODY,{"derivedFrom":makeQuery(id+"F12.opPattern","COPY",BODY,{"derivedFrom":makeQuery(id+"F6.opPattern","COPY",BODY,{"derivedFrom":makeQuery(id+"F4.opPattern","COPY",BODY,{"derivedFrom":makeQuery(id+"F3.opPattern","COPY",BODY,{"derivedFrom":makeQuery(id+"F2.opPattern","COPY",BODY,{"derivedFrom":makeQuery(id+"F1.opRevolve","SWEPT_BODY",BODY,{"disambiguationData":[OSD([sQuery(id+"F0.wireOp",EDGE,"E1")])]}),"instanceName":"1"}),"instanceName":"1"}),"instanceName":"1"}),"instanceName":"1"}),"instanceName":"1"}),"instanceName":"1"});
            var Q2321;
            Q2321=makeQuery(id+"F13.opPattern","COPY",BODY,{"derivedFrom":makeQuery(id+"F12.opPattern","COPY",BODY,{"derivedFrom":makeQuery(id+"F6.opPattern","COPY",BODY,{"derivedFrom":makeQuery(id+"F5.opPattern","COPY",BODY,{"derivedFrom":makeQuery(id+"F1.opRevolve","SWEPT_BODY",BODY,{"disambiguationData":[OSD([sQuery(id+"F0.wireOp",EDGE,"E1")])]}),"instanceName":"1"}),"instanceName":"1"}),"instanceName":"1"}),"instanceName":"1"});
            var Q2322;
            Q2322=makeQuery(id+"F13.opPattern","COPY",BODY,{"derivedFrom":makeQuery(id+"F12.opPattern","COPY",BODY,{"derivedFrom":makeQuery(id+"F6.opPattern","COPY",BODY,{"derivedFrom":makeQuery(id+"F5.opPattern","COPY",BODY,{"derivedFrom":makeQuery(id+"F2.opPattern","COPY",BODY,{"derivedFrom":makeQuery(id+"F1.opRevolve","SWEPT_BODY",BODY,{"disambiguationData":[OSD([sQuery(id+"F0.wireOp",EDGE,"E1")])]}),"instanceName":"1"}),"instanceName":"1"}),"instanceName":"1"}),"instanceName":"1"}),"instanceName":"1"});
            var Q2323;
            Q2323=makeQuery(id+"F13.opPattern","COPY",BODY,{"derivedFrom":makeQuery(id+"F12.opPattern","COPY",BODY,{"derivedFrom":makeQuery(id+"F6.opPattern","COPY",BODY,{"derivedFrom":makeQuery(id+"F5.opPattern","COPY",BODY,{"derivedFrom":makeQuery(id+"F3.opPattern","COPY",BODY,{"derivedFrom":makeQuery(id+"F2.opPattern","COPY",BODY,{"derivedFrom":makeQuery(id+"F1.opRevolve","SWEPT_BODY",BODY,{"disambiguationData":[OSD([sQuery(id+"F0.wireOp",EDGE,"E1")])]}),"instanceName":"1"}),"instanceName":"1"}),"instanceName":"1"}),"instanceName":"1"}),"instanceName":"1"}),"instanceName":"1"});
            var Q2324;
            Q2324=makeQuery(id+"F13.opPattern","COPY",BODY,{"derivedFrom":makeQuery(id+"F12.opPattern","COPY",BODY,{"derivedFrom":makeQuery(id+"F6.opPattern","COPY",BODY,{"derivedFrom":makeQuery(id+"F5.opPattern","COPY",BODY,{"derivedFrom":makeQuery(id+"F4.opPattern","COPY",BODY,{"derivedFrom":makeQuery(id+"F1.opRevolve","SWEPT_BODY",BODY,{"disambiguationData":[OSD([sQuery(id+"F0.wireOp",EDGE,"E1")])]}),"instanceName":"1"}),"instanceName":"1"}),"instanceName":"1"}),"instanceName":"1"}),"instanceName":"1"});
            var Q2325;
            Q2325=makeQuery(id+"F13.opPattern","COPY",BODY,{"derivedFrom":makeQuery(id+"F12.opPattern","COPY",BODY,{"derivedFrom":makeQuery(id+"F6.opPattern","COPY",BODY,{"derivedFrom":makeQuery(id+"F5.opPattern","COPY",BODY,{"derivedFrom":makeQuery(id+"F4.opPattern","COPY",BODY,{"derivedFrom":makeQuery(id+"F2.opPattern","COPY",BODY,{"derivedFrom":makeQuery(id+"F1.opRevolve","SWEPT_BODY",BODY,{"disambiguationData":[OSD([sQuery(id+"F0.wireOp",EDGE,"E1")])]}),"instanceName":"1"}),"instanceName":"1"}),"instanceName":"1"}),"instanceName":"1"}),"instanceName":"1"}),"instanceName":"1"});
            var Q2326;
            Q2326=makeQuery(id+"F13.opPattern","COPY",BODY,{"derivedFrom":makeQuery(id+"F12.opPattern","COPY",BODY,{"derivedFrom":makeQuery(id+"F6.opPattern","COPY",BODY,{"derivedFrom":makeQuery(id+"F5.opPattern","COPY",BODY,{"derivedFrom":makeQuery(id+"F4.opPattern","COPY",BODY,{"derivedFrom":makeQuery(id+"F3.opPattern","COPY",BODY,{"derivedFrom":makeQuery(id+"F2.opPattern","COPY",BODY,{"derivedFrom":makeQuery(id+"F1.opRevolve","SWEPT_BODY",BODY,{"disambiguationData":[OSD([sQuery(id+"F0.wireOp",EDGE,"E1")])]}),"instanceName":"1"}),"instanceName":"1"}),"instanceName":"1"}),"instanceName":"1"}),"instanceName":"1"}),"instanceName":"1"}),"instanceName":"1"});
            var Q2327;
            Q2327=makeQuery(id+"F13.opPattern","COPY",BODY,{"derivedFrom":makeQuery(id+"F12.opPattern","COPY",BODY,{"derivedFrom":makeQuery(id+"F7.opPattern","COPY",BODY,{"derivedFrom":makeQuery(id+"F1.opRevolve","SWEPT_BODY",BODY,{"disambiguationData":[OSD([sQuery(id+"F0.wireOp",EDGE,"E1")])]}),"instanceName":"1"}),"instanceName":"1"}),"instanceName":"1"});
            var Q2328;
            Q2328=makeQuery(id+"F13.opPattern","COPY",BODY,{"derivedFrom":makeQuery(id+"F12.opPattern","COPY",BODY,{"derivedFrom":makeQuery(id+"F7.opPattern","COPY",BODY,{"derivedFrom":makeQuery(id+"F2.opPattern","COPY",BODY,{"derivedFrom":makeQuery(id+"F1.opRevolve","SWEPT_BODY",BODY,{"disambiguationData":[OSD([sQuery(id+"F0.wireOp",EDGE,"E1")])]}),"instanceName":"1"}),"instanceName":"1"}),"instanceName":"1"}),"instanceName":"1"});
            var Q2329;
            Q2329=makeQuery(id+"F13.opPattern","COPY",BODY,{"derivedFrom":makeQuery(id+"F12.opPattern","COPY",BODY,{"derivedFrom":makeQuery(id+"F7.opPattern","COPY",BODY,{"derivedFrom":makeQuery(id+"F3.opPattern","COPY",BODY,{"derivedFrom":makeQuery(id+"F2.opPattern","COPY",BODY,{"derivedFrom":makeQuery(id+"F1.opRevolve","SWEPT_BODY",BODY,{"disambiguationData":[OSD([sQuery(id+"F0.wireOp",EDGE,"E1")])]}),"instanceName":"1"}),"instanceName":"1"}),"instanceName":"1"}),"instanceName":"1"}),"instanceName":"1"});
            var Q2330;
            Q2330=makeQuery(id+"F13.opPattern","COPY",BODY,{"derivedFrom":makeQuery(id+"F12.opPattern","COPY",BODY,{"derivedFrom":makeQuery(id+"F7.opPattern","COPY",BODY,{"derivedFrom":makeQuery(id+"F4.opPattern","COPY",BODY,{"derivedFrom":makeQuery(id+"F1.opRevolve","SWEPT_BODY",BODY,{"disambiguationData":[OSD([sQuery(id+"F0.wireOp",EDGE,"E1")])]}),"instanceName":"1"}),"instanceName":"1"}),"instanceName":"1"}),"instanceName":"1"});
            var Q2331;
            Q2331=makeQuery(id+"F13.opPattern","COPY",BODY,{"derivedFrom":makeQuery(id+"F12.opPattern","COPY",BODY,{"derivedFrom":makeQuery(id+"F7.opPattern","COPY",BODY,{"derivedFrom":makeQuery(id+"F4.opPattern","COPY",BODY,{"derivedFrom":makeQuery(id+"F2.opPattern","COPY",BODY,{"derivedFrom":makeQuery(id+"F1.opRevolve","SWEPT_BODY",BODY,{"disambiguationData":[OSD([sQuery(id+"F0.wireOp",EDGE,"E1")])]}),"instanceName":"1"}),"instanceName":"1"}),"instanceName":"1"}),"instanceName":"1"}),"instanceName":"1"});
            var Q2332;
            Q2332=makeQuery(id+"F13.opPattern","COPY",BODY,{"derivedFrom":makeQuery(id+"F12.opPattern","COPY",BODY,{"derivedFrom":makeQuery(id+"F7.opPattern","COPY",BODY,{"derivedFrom":makeQuery(id+"F4.opPattern","COPY",BODY,{"derivedFrom":makeQuery(id+"F3.opPattern","COPY",BODY,{"derivedFrom":makeQuery(id+"F2.opPattern","COPY",BODY,{"derivedFrom":makeQuery(id+"F1.opRevolve","SWEPT_BODY",BODY,{"disambiguationData":[OSD([sQuery(id+"F0.wireOp",EDGE,"E1")])]}),"instanceName":"1"}),"instanceName":"1"}),"instanceName":"1"}),"instanceName":"1"}),"instanceName":"1"}),"instanceName":"1"});
            var Q2333;
            Q2333=makeQuery(id+"F13.opPattern","COPY",BODY,{"derivedFrom":makeQuery(id+"F12.opPattern","COPY",BODY,{"derivedFrom":makeQuery(id+"F7.opPattern","COPY",BODY,{"derivedFrom":makeQuery(id+"F5.opPattern","COPY",BODY,{"derivedFrom":makeQuery(id+"F1.opRevolve","SWEPT_BODY",BODY,{"disambiguationData":[OSD([sQuery(id+"F0.wireOp",EDGE,"E1")])]}),"instanceName":"1"}),"instanceName":"1"}),"instanceName":"1"}),"instanceName":"1"});
            var Q2334;
            Q2334=makeQuery(id+"F13.opPattern","COPY",BODY,{"derivedFrom":makeQuery(id+"F12.opPattern","COPY",BODY,{"derivedFrom":makeQuery(id+"F7.opPattern","COPY",BODY,{"derivedFrom":makeQuery(id+"F5.opPattern","COPY",BODY,{"derivedFrom":makeQuery(id+"F2.opPattern","COPY",BODY,{"derivedFrom":makeQuery(id+"F1.opRevolve","SWEPT_BODY",BODY,{"disambiguationData":[OSD([sQuery(id+"F0.wireOp",EDGE,"E1")])]}),"instanceName":"1"}),"instanceName":"1"}),"instanceName":"1"}),"instanceName":"1"}),"instanceName":"1"});
            var Q2335;
            Q2335=makeQuery(id+"F13.opPattern","COPY",BODY,{"derivedFrom":makeQuery(id+"F12.opPattern","COPY",BODY,{"derivedFrom":makeQuery(id+"F7.opPattern","COPY",BODY,{"derivedFrom":makeQuery(id+"F5.opPattern","COPY",BODY,{"derivedFrom":makeQuery(id+"F3.opPattern","COPY",BODY,{"derivedFrom":makeQuery(id+"F2.opPattern","COPY",BODY,{"derivedFrom":makeQuery(id+"F1.opRevolve","SWEPT_BODY",BODY,{"disambiguationData":[OSD([sQuery(id+"F0.wireOp",EDGE,"E1")])]}),"instanceName":"1"}),"instanceName":"1"}),"instanceName":"1"}),"instanceName":"1"}),"instanceName":"1"}),"instanceName":"1"});
            var Q2336;
            Q2336=makeQuery(id+"F13.opPattern","COPY",BODY,{"derivedFrom":makeQuery(id+"F12.opPattern","COPY",BODY,{"derivedFrom":makeQuery(id+"F7.opPattern","COPY",BODY,{"derivedFrom":makeQuery(id+"F5.opPattern","COPY",BODY,{"derivedFrom":makeQuery(id+"F4.opPattern","COPY",BODY,{"derivedFrom":makeQuery(id+"F1.opRevolve","SWEPT_BODY",BODY,{"disambiguationData":[OSD([sQuery(id+"F0.wireOp",EDGE,"E1")])]}),"instanceName":"1"}),"instanceName":"1"}),"instanceName":"1"}),"instanceName":"1"}),"instanceName":"1"});
            var Q2337;
            Q2337=makeQuery(id+"F13.opPattern","COPY",BODY,{"derivedFrom":makeQuery(id+"F12.opPattern","COPY",BODY,{"derivedFrom":makeQuery(id+"F7.opPattern","COPY",BODY,{"derivedFrom":makeQuery(id+"F5.opPattern","COPY",BODY,{"derivedFrom":makeQuery(id+"F4.opPattern","COPY",BODY,{"derivedFrom":makeQuery(id+"F2.opPattern","COPY",BODY,{"derivedFrom":makeQuery(id+"F1.opRevolve","SWEPT_BODY",BODY,{"disambiguationData":[OSD([sQuery(id+"F0.wireOp",EDGE,"E1")])]}),"instanceName":"1"}),"instanceName":"1"}),"instanceName":"1"}),"instanceName":"1"}),"instanceName":"1"}),"instanceName":"1"});
            var Q2338;
            Q2338=makeQuery(id+"F13.opPattern","COPY",BODY,{"derivedFrom":makeQuery(id+"F12.opPattern","COPY",BODY,{"derivedFrom":makeQuery(id+"F7.opPattern","COPY",BODY,{"derivedFrom":makeQuery(id+"F5.opPattern","COPY",BODY,{"derivedFrom":makeQuery(id+"F4.opPattern","COPY",BODY,{"derivedFrom":makeQuery(id+"F3.opPattern","COPY",BODY,{"derivedFrom":makeQuery(id+"F2.opPattern","COPY",BODY,{"derivedFrom":makeQuery(id+"F1.opRevolve","SWEPT_BODY",BODY,{"disambiguationData":[OSD([sQuery(id+"F0.wireOp",EDGE,"E1")])]}),"instanceName":"1"}),"instanceName":"1"}),"instanceName":"1"}),"instanceName":"1"}),"instanceName":"1"}),"instanceName":"1"}),"instanceName":"1"});
            var Q2339;
            Q2339=makeQuery(id+"F13.opPattern","COPY",BODY,{"derivedFrom":makeQuery(id+"F12.opPattern","COPY",BODY,{"derivedFrom":makeQuery(id+"F7.opPattern","COPY",BODY,{"derivedFrom":makeQuery(id+"F6.opPattern","COPY",BODY,{"derivedFrom":makeQuery(id+"F1.opRevolve","SWEPT_BODY",BODY,{"disambiguationData":[OSD([sQuery(id+"F0.wireOp",EDGE,"E1")])]}),"instanceName":"1"}),"instanceName":"1"}),"instanceName":"1"}),"instanceName":"1"});
            var Q2340;
            Q2340=makeQuery(id+"F13.opPattern","COPY",BODY,{"derivedFrom":makeQuery(id+"F12.opPattern","COPY",BODY,{"derivedFrom":makeQuery(id+"F7.opPattern","COPY",BODY,{"derivedFrom":makeQuery(id+"F6.opPattern","COPY",BODY,{"derivedFrom":makeQuery(id+"F2.opPattern","COPY",BODY,{"derivedFrom":makeQuery(id+"F1.opRevolve","SWEPT_BODY",BODY,{"disambiguationData":[OSD([sQuery(id+"F0.wireOp",EDGE,"E1")])]}),"instanceName":"1"}),"instanceName":"1"}),"instanceName":"1"}),"instanceName":"1"}),"instanceName":"1"});
            var Q2341;
            Q2341=makeQuery(id+"F13.opPattern","COPY",BODY,{"derivedFrom":makeQuery(id+"F12.opPattern","COPY",BODY,{"derivedFrom":makeQuery(id+"F7.opPattern","COPY",BODY,{"derivedFrom":makeQuery(id+"F6.opPattern","COPY",BODY,{"derivedFrom":makeQuery(id+"F3.opPattern","COPY",BODY,{"derivedFrom":makeQuery(id+"F2.opPattern","COPY",BODY,{"derivedFrom":makeQuery(id+"F1.opRevolve","SWEPT_BODY",BODY,{"disambiguationData":[OSD([sQuery(id+"F0.wireOp",EDGE,"E1")])]}),"instanceName":"1"}),"instanceName":"1"}),"instanceName":"1"}),"instanceName":"1"}),"instanceName":"1"}),"instanceName":"1"});
            var Q2342;
            Q2342=makeQuery(id+"F13.opPattern","COPY",BODY,{"derivedFrom":makeQuery(id+"F12.opPattern","COPY",BODY,{"derivedFrom":makeQuery(id+"F7.opPattern","COPY",BODY,{"derivedFrom":makeQuery(id+"F6.opPattern","COPY",BODY,{"derivedFrom":makeQuery(id+"F4.opPattern","COPY",BODY,{"derivedFrom":makeQuery(id+"F1.opRevolve","SWEPT_BODY",BODY,{"disambiguationData":[OSD([sQuery(id+"F0.wireOp",EDGE,"E1")])]}),"instanceName":"1"}),"instanceName":"1"}),"instanceName":"1"}),"instanceName":"1"}),"instanceName":"1"});
            var Q2343;
            Q2343=makeQuery(id+"F13.opPattern","COPY",BODY,{"derivedFrom":makeQuery(id+"F12.opPattern","COPY",BODY,{"derivedFrom":makeQuery(id+"F7.opPattern","COPY",BODY,{"derivedFrom":makeQuery(id+"F6.opPattern","COPY",BODY,{"derivedFrom":makeQuery(id+"F4.opPattern","COPY",BODY,{"derivedFrom":makeQuery(id+"F2.opPattern","COPY",BODY,{"derivedFrom":makeQuery(id+"F1.opRevolve","SWEPT_BODY",BODY,{"disambiguationData":[OSD([sQuery(id+"F0.wireOp",EDGE,"E1")])]}),"instanceName":"1"}),"instanceName":"1"}),"instanceName":"1"}),"instanceName":"1"}),"instanceName":"1"}),"instanceName":"1"});
            var Q2344;
            Q2344=makeQuery(id+"F13.opPattern","COPY",BODY,{"derivedFrom":makeQuery(id+"F12.opPattern","COPY",BODY,{"derivedFrom":makeQuery(id+"F7.opPattern","COPY",BODY,{"derivedFrom":makeQuery(id+"F6.opPattern","COPY",BODY,{"derivedFrom":makeQuery(id+"F4.opPattern","COPY",BODY,{"derivedFrom":makeQuery(id+"F3.opPattern","COPY",BODY,{"derivedFrom":makeQuery(id+"F2.opPattern","COPY",BODY,{"derivedFrom":makeQuery(id+"F1.opRevolve","SWEPT_BODY",BODY,{"disambiguationData":[OSD([sQuery(id+"F0.wireOp",EDGE,"E1")])]}),"instanceName":"1"}),"instanceName":"1"}),"instanceName":"1"}),"instanceName":"1"}),"instanceName":"1"}),"instanceName":"1"}),"instanceName":"1"});
            var Q2345;
            Q2345=makeQuery(id+"F13.opPattern","COPY",BODY,{"derivedFrom":makeQuery(id+"F12.opPattern","COPY",BODY,{"derivedFrom":makeQuery(id+"F7.opPattern","COPY",BODY,{"derivedFrom":makeQuery(id+"F6.opPattern","COPY",BODY,{"derivedFrom":makeQuery(id+"F5.opPattern","COPY",BODY,{"derivedFrom":makeQuery(id+"F1.opRevolve","SWEPT_BODY",BODY,{"disambiguationData":[OSD([sQuery(id+"F0.wireOp",EDGE,"E1")])]}),"instanceName":"1"}),"instanceName":"1"}),"instanceName":"1"}),"instanceName":"1"}),"instanceName":"1"});
            var Q2346;
            Q2346=makeQuery(id+"F13.opPattern","COPY",BODY,{"derivedFrom":makeQuery(id+"F12.opPattern","COPY",BODY,{"derivedFrom":makeQuery(id+"F7.opPattern","COPY",BODY,{"derivedFrom":makeQuery(id+"F6.opPattern","COPY",BODY,{"derivedFrom":makeQuery(id+"F5.opPattern","COPY",BODY,{"derivedFrom":makeQuery(id+"F2.opPattern","COPY",BODY,{"derivedFrom":makeQuery(id+"F1.opRevolve","SWEPT_BODY",BODY,{"disambiguationData":[OSD([sQuery(id+"F0.wireOp",EDGE,"E1")])]}),"instanceName":"1"}),"instanceName":"1"}),"instanceName":"1"}),"instanceName":"1"}),"instanceName":"1"}),"instanceName":"1"});
            var Q2347;
            Q2347=makeQuery(id+"F13.opPattern","COPY",BODY,{"derivedFrom":makeQuery(id+"F12.opPattern","COPY",BODY,{"derivedFrom":makeQuery(id+"F7.opPattern","COPY",BODY,{"derivedFrom":makeQuery(id+"F6.opPattern","COPY",BODY,{"derivedFrom":makeQuery(id+"F5.opPattern","COPY",BODY,{"derivedFrom":makeQuery(id+"F3.opPattern","COPY",BODY,{"derivedFrom":makeQuery(id+"F2.opPattern","COPY",BODY,{"derivedFrom":makeQuery(id+"F1.opRevolve","SWEPT_BODY",BODY,{"disambiguationData":[OSD([sQuery(id+"F0.wireOp",EDGE,"E1")])]}),"instanceName":"1"}),"instanceName":"1"}),"instanceName":"1"}),"instanceName":"1"}),"instanceName":"1"}),"instanceName":"1"}),"instanceName":"1"});
            var Q2348;
            Q2348=makeQuery(id+"F13.opPattern","COPY",BODY,{"derivedFrom":makeQuery(id+"F12.opPattern","COPY",BODY,{"derivedFrom":makeQuery(id+"F7.opPattern","COPY",BODY,{"derivedFrom":makeQuery(id+"F6.opPattern","COPY",BODY,{"derivedFrom":makeQuery(id+"F5.opPattern","COPY",BODY,{"derivedFrom":makeQuery(id+"F4.opPattern","COPY",BODY,{"derivedFrom":makeQuery(id+"F1.opRevolve","SWEPT_BODY",BODY,{"disambiguationData":[OSD([sQuery(id+"F0.wireOp",EDGE,"E1")])]}),"instanceName":"1"}),"instanceName":"1"}),"instanceName":"1"}),"instanceName":"1"}),"instanceName":"1"}),"instanceName":"1"});
            var Q2349;
            Q2349=makeQuery(id+"F13.opPattern","COPY",BODY,{"derivedFrom":makeQuery(id+"F12.opPattern","COPY",BODY,{"derivedFrom":makeQuery(id+"F7.opPattern","COPY",BODY,{"derivedFrom":makeQuery(id+"F6.opPattern","COPY",BODY,{"derivedFrom":makeQuery(id+"F5.opPattern","COPY",BODY,{"derivedFrom":makeQuery(id+"F4.opPattern","COPY",BODY,{"derivedFrom":makeQuery(id+"F2.opPattern","COPY",BODY,{"derivedFrom":makeQuery(id+"F1.opRevolve","SWEPT_BODY",BODY,{"disambiguationData":[OSD([sQuery(id+"F0.wireOp",EDGE,"E1")])]}),"instanceName":"1"}),"instanceName":"1"}),"instanceName":"1"}),"instanceName":"1"}),"instanceName":"1"}),"instanceName":"1"}),"instanceName":"1"});
            var Q2350;
            Q2350=makeQuery(id+"F13.opPattern","COPY",BODY,{"derivedFrom":makeQuery(id+"F12.opPattern","COPY",BODY,{"derivedFrom":makeQuery(id+"F7.opPattern","COPY",BODY,{"derivedFrom":makeQuery(id+"F6.opPattern","COPY",BODY,{"derivedFrom":makeQuery(id+"F5.opPattern","COPY",BODY,{"derivedFrom":makeQuery(id+"F4.opPattern","COPY",BODY,{"derivedFrom":makeQuery(id+"F3.opPattern","COPY",BODY,{"derivedFrom":makeQuery(id+"F2.opPattern","COPY",BODY,{"derivedFrom":makeQuery(id+"F1.opRevolve","SWEPT_BODY",BODY,{"disambiguationData":[OSD([sQuery(id+"F0.wireOp",EDGE,"E1")])]}),"instanceName":"1"}),"instanceName":"1"}),"instanceName":"1"}),"instanceName":"1"}),"instanceName":"1"}),"instanceName":"1"}),"instanceName":"1"}),"instanceName":"1"});
            var Q2351;
            Q2351=makeQuery(id+"F13.opPattern","COPY",BODY,{"derivedFrom":makeQuery(id+"F12.opPattern","COPY",BODY,{"derivedFrom":makeQuery(id+"F8.opPattern","COPY",BODY,{"derivedFrom":makeQuery(id+"F1.opRevolve","SWEPT_BODY",BODY,{"disambiguationData":[OSD([sQuery(id+"F0.wireOp",EDGE,"E1")])]}),"instanceName":"1"}),"instanceName":"1"}),"instanceName":"1"});
            var Q2352;
            Q2352=makeQuery(id+"F13.opPattern","COPY",BODY,{"derivedFrom":makeQuery(id+"F12.opPattern","COPY",BODY,{"derivedFrom":makeQuery(id+"F8.opPattern","COPY",BODY,{"derivedFrom":makeQuery(id+"F2.opPattern","COPY",BODY,{"derivedFrom":makeQuery(id+"F1.opRevolve","SWEPT_BODY",BODY,{"disambiguationData":[OSD([sQuery(id+"F0.wireOp",EDGE,"E1")])]}),"instanceName":"1"}),"instanceName":"1"}),"instanceName":"1"}),"instanceName":"1"});
            var Q2353;
            Q2353=makeQuery(id+"F13.opPattern","COPY",BODY,{"derivedFrom":makeQuery(id+"F12.opPattern","COPY",BODY,{"derivedFrom":makeQuery(id+"F8.opPattern","COPY",BODY,{"derivedFrom":makeQuery(id+"F3.opPattern","COPY",BODY,{"derivedFrom":makeQuery(id+"F2.opPattern","COPY",BODY,{"derivedFrom":makeQuery(id+"F1.opRevolve","SWEPT_BODY",BODY,{"disambiguationData":[OSD([sQuery(id+"F0.wireOp",EDGE,"E1")])]}),"instanceName":"1"}),"instanceName":"1"}),"instanceName":"1"}),"instanceName":"1"}),"instanceName":"1"});
            var Q2354;
            Q2354=makeQuery(id+"F13.opPattern","COPY",BODY,{"derivedFrom":makeQuery(id+"F12.opPattern","COPY",BODY,{"derivedFrom":makeQuery(id+"F8.opPattern","COPY",BODY,{"derivedFrom":makeQuery(id+"F4.opPattern","COPY",BODY,{"derivedFrom":makeQuery(id+"F1.opRevolve","SWEPT_BODY",BODY,{"disambiguationData":[OSD([sQuery(id+"F0.wireOp",EDGE,"E1")])]}),"instanceName":"1"}),"instanceName":"1"}),"instanceName":"1"}),"instanceName":"1"});
            var Q2355;
            Q2355=makeQuery(id+"F13.opPattern","COPY",BODY,{"derivedFrom":makeQuery(id+"F12.opPattern","COPY",BODY,{"derivedFrom":makeQuery(id+"F8.opPattern","COPY",BODY,{"derivedFrom":makeQuery(id+"F4.opPattern","COPY",BODY,{"derivedFrom":makeQuery(id+"F2.opPattern","COPY",BODY,{"derivedFrom":makeQuery(id+"F1.opRevolve","SWEPT_BODY",BODY,{"disambiguationData":[OSD([sQuery(id+"F0.wireOp",EDGE,"E1")])]}),"instanceName":"1"}),"instanceName":"1"}),"instanceName":"1"}),"instanceName":"1"}),"instanceName":"1"});
            var Q2356;
            Q2356=makeQuery(id+"F13.opPattern","COPY",BODY,{"derivedFrom":makeQuery(id+"F12.opPattern","COPY",BODY,{"derivedFrom":makeQuery(id+"F8.opPattern","COPY",BODY,{"derivedFrom":makeQuery(id+"F4.opPattern","COPY",BODY,{"derivedFrom":makeQuery(id+"F3.opPattern","COPY",BODY,{"derivedFrom":makeQuery(id+"F2.opPattern","COPY",BODY,{"derivedFrom":makeQuery(id+"F1.opRevolve","SWEPT_BODY",BODY,{"disambiguationData":[OSD([sQuery(id+"F0.wireOp",EDGE,"E1")])]}),"instanceName":"1"}),"instanceName":"1"}),"instanceName":"1"}),"instanceName":"1"}),"instanceName":"1"}),"instanceName":"1"});
            var Q2357;
            Q2357=makeQuery(id+"F13.opPattern","COPY",BODY,{"derivedFrom":makeQuery(id+"F12.opPattern","COPY",BODY,{"derivedFrom":makeQuery(id+"F8.opPattern","COPY",BODY,{"derivedFrom":makeQuery(id+"F5.opPattern","COPY",BODY,{"derivedFrom":makeQuery(id+"F1.opRevolve","SWEPT_BODY",BODY,{"disambiguationData":[OSD([sQuery(id+"F0.wireOp",EDGE,"E1")])]}),"instanceName":"1"}),"instanceName":"1"}),"instanceName":"1"}),"instanceName":"1"});
            var Q2358;
            Q2358=makeQuery(id+"F13.opPattern","COPY",BODY,{"derivedFrom":makeQuery(id+"F12.opPattern","COPY",BODY,{"derivedFrom":makeQuery(id+"F8.opPattern","COPY",BODY,{"derivedFrom":makeQuery(id+"F5.opPattern","COPY",BODY,{"derivedFrom":makeQuery(id+"F2.opPattern","COPY",BODY,{"derivedFrom":makeQuery(id+"F1.opRevolve","SWEPT_BODY",BODY,{"disambiguationData":[OSD([sQuery(id+"F0.wireOp",EDGE,"E1")])]}),"instanceName":"1"}),"instanceName":"1"}),"instanceName":"1"}),"instanceName":"1"}),"instanceName":"1"});
            var Q2359;
            Q2359=makeQuery(id+"F13.opPattern","COPY",BODY,{"derivedFrom":makeQuery(id+"F12.opPattern","COPY",BODY,{"derivedFrom":makeQuery(id+"F8.opPattern","COPY",BODY,{"derivedFrom":makeQuery(id+"F5.opPattern","COPY",BODY,{"derivedFrom":makeQuery(id+"F3.opPattern","COPY",BODY,{"derivedFrom":makeQuery(id+"F2.opPattern","COPY",BODY,{"derivedFrom":makeQuery(id+"F1.opRevolve","SWEPT_BODY",BODY,{"disambiguationData":[OSD([sQuery(id+"F0.wireOp",EDGE,"E1")])]}),"instanceName":"1"}),"instanceName":"1"}),"instanceName":"1"}),"instanceName":"1"}),"instanceName":"1"}),"instanceName":"1"});
            var Q2360;
            Q2360=makeQuery(id+"F13.opPattern","COPY",BODY,{"derivedFrom":makeQuery(id+"F12.opPattern","COPY",BODY,{"derivedFrom":makeQuery(id+"F8.opPattern","COPY",BODY,{"derivedFrom":makeQuery(id+"F5.opPattern","COPY",BODY,{"derivedFrom":makeQuery(id+"F4.opPattern","COPY",BODY,{"derivedFrom":makeQuery(id+"F1.opRevolve","SWEPT_BODY",BODY,{"disambiguationData":[OSD([sQuery(id+"F0.wireOp",EDGE,"E1")])]}),"instanceName":"1"}),"instanceName":"1"}),"instanceName":"1"}),"instanceName":"1"}),"instanceName":"1"});
            var Q2361;
            Q2361=makeQuery(id+"F13.opPattern","COPY",BODY,{"derivedFrom":makeQuery(id+"F12.opPattern","COPY",BODY,{"derivedFrom":makeQuery(id+"F8.opPattern","COPY",BODY,{"derivedFrom":makeQuery(id+"F5.opPattern","COPY",BODY,{"derivedFrom":makeQuery(id+"F4.opPattern","COPY",BODY,{"derivedFrom":makeQuery(id+"F2.opPattern","COPY",BODY,{"derivedFrom":makeQuery(id+"F1.opRevolve","SWEPT_BODY",BODY,{"disambiguationData":[OSD([sQuery(id+"F0.wireOp",EDGE,"E1")])]}),"instanceName":"1"}),"instanceName":"1"}),"instanceName":"1"}),"instanceName":"1"}),"instanceName":"1"}),"instanceName":"1"});
            var Q2362;
            Q2362=makeQuery(id+"F13.opPattern","COPY",BODY,{"derivedFrom":makeQuery(id+"F12.opPattern","COPY",BODY,{"derivedFrom":makeQuery(id+"F8.opPattern","COPY",BODY,{"derivedFrom":makeQuery(id+"F5.opPattern","COPY",BODY,{"derivedFrom":makeQuery(id+"F4.opPattern","COPY",BODY,{"derivedFrom":makeQuery(id+"F3.opPattern","COPY",BODY,{"derivedFrom":makeQuery(id+"F2.opPattern","COPY",BODY,{"derivedFrom":makeQuery(id+"F1.opRevolve","SWEPT_BODY",BODY,{"disambiguationData":[OSD([sQuery(id+"F0.wireOp",EDGE,"E1")])]}),"instanceName":"1"}),"instanceName":"1"}),"instanceName":"1"}),"instanceName":"1"}),"instanceName":"1"}),"instanceName":"1"}),"instanceName":"1"});
            var Q2363;
            Q2363=makeQuery(id+"F13.opPattern","COPY",BODY,{"derivedFrom":makeQuery(id+"F12.opPattern","COPY",BODY,{"derivedFrom":makeQuery(id+"F8.opPattern","COPY",BODY,{"derivedFrom":makeQuery(id+"F6.opPattern","COPY",BODY,{"derivedFrom":makeQuery(id+"F1.opRevolve","SWEPT_BODY",BODY,{"disambiguationData":[OSD([sQuery(id+"F0.wireOp",EDGE,"E1")])]}),"instanceName":"1"}),"instanceName":"1"}),"instanceName":"1"}),"instanceName":"1"});
            var Q2364;
            Q2364=makeQuery(id+"F13.opPattern","COPY",BODY,{"derivedFrom":makeQuery(id+"F12.opPattern","COPY",BODY,{"derivedFrom":makeQuery(id+"F8.opPattern","COPY",BODY,{"derivedFrom":makeQuery(id+"F6.opPattern","COPY",BODY,{"derivedFrom":makeQuery(id+"F2.opPattern","COPY",BODY,{"derivedFrom":makeQuery(id+"F1.opRevolve","SWEPT_BODY",BODY,{"disambiguationData":[OSD([sQuery(id+"F0.wireOp",EDGE,"E1")])]}),"instanceName":"1"}),"instanceName":"1"}),"instanceName":"1"}),"instanceName":"1"}),"instanceName":"1"});
            var Q2365;
            Q2365=makeQuery(id+"F13.opPattern","COPY",BODY,{"derivedFrom":makeQuery(id+"F12.opPattern","COPY",BODY,{"derivedFrom":makeQuery(id+"F8.opPattern","COPY",BODY,{"derivedFrom":makeQuery(id+"F6.opPattern","COPY",BODY,{"derivedFrom":makeQuery(id+"F3.opPattern","COPY",BODY,{"derivedFrom":makeQuery(id+"F2.opPattern","COPY",BODY,{"derivedFrom":makeQuery(id+"F1.opRevolve","SWEPT_BODY",BODY,{"disambiguationData":[OSD([sQuery(id+"F0.wireOp",EDGE,"E1")])]}),"instanceName":"1"}),"instanceName":"1"}),"instanceName":"1"}),"instanceName":"1"}),"instanceName":"1"}),"instanceName":"1"});
            var Q2366;
            Q2366=makeQuery(id+"F13.opPattern","COPY",BODY,{"derivedFrom":makeQuery(id+"F12.opPattern","COPY",BODY,{"derivedFrom":makeQuery(id+"F8.opPattern","COPY",BODY,{"derivedFrom":makeQuery(id+"F6.opPattern","COPY",BODY,{"derivedFrom":makeQuery(id+"F4.opPattern","COPY",BODY,{"derivedFrom":makeQuery(id+"F1.opRevolve","SWEPT_BODY",BODY,{"disambiguationData":[OSD([sQuery(id+"F0.wireOp",EDGE,"E1")])]}),"instanceName":"1"}),"instanceName":"1"}),"instanceName":"1"}),"instanceName":"1"}),"instanceName":"1"});
            var Q2367;
            Q2367=makeQuery(id+"F13.opPattern","COPY",BODY,{"derivedFrom":makeQuery(id+"F12.opPattern","COPY",BODY,{"derivedFrom":makeQuery(id+"F8.opPattern","COPY",BODY,{"derivedFrom":makeQuery(id+"F6.opPattern","COPY",BODY,{"derivedFrom":makeQuery(id+"F4.opPattern","COPY",BODY,{"derivedFrom":makeQuery(id+"F2.opPattern","COPY",BODY,{"derivedFrom":makeQuery(id+"F1.opRevolve","SWEPT_BODY",BODY,{"disambiguationData":[OSD([sQuery(id+"F0.wireOp",EDGE,"E1")])]}),"instanceName":"1"}),"instanceName":"1"}),"instanceName":"1"}),"instanceName":"1"}),"instanceName":"1"}),"instanceName":"1"});
            var Q2368;
            Q2368=makeQuery(id+"F13.opPattern","COPY",BODY,{"derivedFrom":makeQuery(id+"F12.opPattern","COPY",BODY,{"derivedFrom":makeQuery(id+"F8.opPattern","COPY",BODY,{"derivedFrom":makeQuery(id+"F6.opPattern","COPY",BODY,{"derivedFrom":makeQuery(id+"F4.opPattern","COPY",BODY,{"derivedFrom":makeQuery(id+"F3.opPattern","COPY",BODY,{"derivedFrom":makeQuery(id+"F2.opPattern","COPY",BODY,{"derivedFrom":makeQuery(id+"F1.opRevolve","SWEPT_BODY",BODY,{"disambiguationData":[OSD([sQuery(id+"F0.wireOp",EDGE,"E1")])]}),"instanceName":"1"}),"instanceName":"1"}),"instanceName":"1"}),"instanceName":"1"}),"instanceName":"1"}),"instanceName":"1"}),"instanceName":"1"});
            var Q2369;
            Q2369=makeQuery(id+"F13.opPattern","COPY",BODY,{"derivedFrom":makeQuery(id+"F12.opPattern","COPY",BODY,{"derivedFrom":makeQuery(id+"F8.opPattern","COPY",BODY,{"derivedFrom":makeQuery(id+"F6.opPattern","COPY",BODY,{"derivedFrom":makeQuery(id+"F5.opPattern","COPY",BODY,{"derivedFrom":makeQuery(id+"F1.opRevolve","SWEPT_BODY",BODY,{"disambiguationData":[OSD([sQuery(id+"F0.wireOp",EDGE,"E1")])]}),"instanceName":"1"}),"instanceName":"1"}),"instanceName":"1"}),"instanceName":"1"}),"instanceName":"1"});
            var Q2370;
            Q2370=makeQuery(id+"F13.opPattern","COPY",BODY,{"derivedFrom":makeQuery(id+"F12.opPattern","COPY",BODY,{"derivedFrom":makeQuery(id+"F8.opPattern","COPY",BODY,{"derivedFrom":makeQuery(id+"F6.opPattern","COPY",BODY,{"derivedFrom":makeQuery(id+"F5.opPattern","COPY",BODY,{"derivedFrom":makeQuery(id+"F2.opPattern","COPY",BODY,{"derivedFrom":makeQuery(id+"F1.opRevolve","SWEPT_BODY",BODY,{"disambiguationData":[OSD([sQuery(id+"F0.wireOp",EDGE,"E1")])]}),"instanceName":"1"}),"instanceName":"1"}),"instanceName":"1"}),"instanceName":"1"}),"instanceName":"1"}),"instanceName":"1"});
            var Q2371;
            Q2371=makeQuery(id+"F13.opPattern","COPY",BODY,{"derivedFrom":makeQuery(id+"F12.opPattern","COPY",BODY,{"derivedFrom":makeQuery(id+"F8.opPattern","COPY",BODY,{"derivedFrom":makeQuery(id+"F6.opPattern","COPY",BODY,{"derivedFrom":makeQuery(id+"F5.opPattern","COPY",BODY,{"derivedFrom":makeQuery(id+"F3.opPattern","COPY",BODY,{"derivedFrom":makeQuery(id+"F2.opPattern","COPY",BODY,{"derivedFrom":makeQuery(id+"F1.opRevolve","SWEPT_BODY",BODY,{"disambiguationData":[OSD([sQuery(id+"F0.wireOp",EDGE,"E1")])]}),"instanceName":"1"}),"instanceName":"1"}),"instanceName":"1"}),"instanceName":"1"}),"instanceName":"1"}),"instanceName":"1"}),"instanceName":"1"});
            var Q2372;
            Q2372=makeQuery(id+"F13.opPattern","COPY",BODY,{"derivedFrom":makeQuery(id+"F12.opPattern","COPY",BODY,{"derivedFrom":makeQuery(id+"F8.opPattern","COPY",BODY,{"derivedFrom":makeQuery(id+"F6.opPattern","COPY",BODY,{"derivedFrom":makeQuery(id+"F5.opPattern","COPY",BODY,{"derivedFrom":makeQuery(id+"F4.opPattern","COPY",BODY,{"derivedFrom":makeQuery(id+"F1.opRevolve","SWEPT_BODY",BODY,{"disambiguationData":[OSD([sQuery(id+"F0.wireOp",EDGE,"E1")])]}),"instanceName":"1"}),"instanceName":"1"}),"instanceName":"1"}),"instanceName":"1"}),"instanceName":"1"}),"instanceName":"1"});
            var Q2373;
            Q2373=makeQuery(id+"F13.opPattern","COPY",BODY,{"derivedFrom":makeQuery(id+"F12.opPattern","COPY",BODY,{"derivedFrom":makeQuery(id+"F8.opPattern","COPY",BODY,{"derivedFrom":makeQuery(id+"F6.opPattern","COPY",BODY,{"derivedFrom":makeQuery(id+"F5.opPattern","COPY",BODY,{"derivedFrom":makeQuery(id+"F4.opPattern","COPY",BODY,{"derivedFrom":makeQuery(id+"F2.opPattern","COPY",BODY,{"derivedFrom":makeQuery(id+"F1.opRevolve","SWEPT_BODY",BODY,{"disambiguationData":[OSD([sQuery(id+"F0.wireOp",EDGE,"E1")])]}),"instanceName":"1"}),"instanceName":"1"}),"instanceName":"1"}),"instanceName":"1"}),"instanceName":"1"}),"instanceName":"1"}),"instanceName":"1"});
            var Q2374;
            Q2374=makeQuery(id+"F13.opPattern","COPY",BODY,{"derivedFrom":makeQuery(id+"F12.opPattern","COPY",BODY,{"derivedFrom":makeQuery(id+"F8.opPattern","COPY",BODY,{"derivedFrom":makeQuery(id+"F6.opPattern","COPY",BODY,{"derivedFrom":makeQuery(id+"F5.opPattern","COPY",BODY,{"derivedFrom":makeQuery(id+"F4.opPattern","COPY",BODY,{"derivedFrom":makeQuery(id+"F3.opPattern","COPY",BODY,{"derivedFrom":makeQuery(id+"F2.opPattern","COPY",BODY,{"derivedFrom":makeQuery(id+"F1.opRevolve","SWEPT_BODY",BODY,{"disambiguationData":[OSD([sQuery(id+"F0.wireOp",EDGE,"E1")])]}),"instanceName":"1"}),"instanceName":"1"}),"instanceName":"1"}),"instanceName":"1"}),"instanceName":"1"}),"instanceName":"1"}),"instanceName":"1"}),"instanceName":"1"});
            var Q2375;
            Q2375=makeQuery(id+"F13.opPattern","COPY",BODY,{"derivedFrom":makeQuery(id+"F12.opPattern","COPY",BODY,{"derivedFrom":makeQuery(id+"F8.opPattern","COPY",BODY,{"derivedFrom":makeQuery(id+"F7.opPattern","COPY",BODY,{"derivedFrom":makeQuery(id+"F1.opRevolve","SWEPT_BODY",BODY,{"disambiguationData":[OSD([sQuery(id+"F0.wireOp",EDGE,"E1")])]}),"instanceName":"1"}),"instanceName":"1"}),"instanceName":"1"}),"instanceName":"1"});
            var Q2376;
            Q2376=makeQuery(id+"F13.opPattern","COPY",BODY,{"derivedFrom":makeQuery(id+"F12.opPattern","COPY",BODY,{"derivedFrom":makeQuery(id+"F8.opPattern","COPY",BODY,{"derivedFrom":makeQuery(id+"F7.opPattern","COPY",BODY,{"derivedFrom":makeQuery(id+"F2.opPattern","COPY",BODY,{"derivedFrom":makeQuery(id+"F1.opRevolve","SWEPT_BODY",BODY,{"disambiguationData":[OSD([sQuery(id+"F0.wireOp",EDGE,"E1")])]}),"instanceName":"1"}),"instanceName":"1"}),"instanceName":"1"}),"instanceName":"1"}),"instanceName":"1"});
            var Q2377;
            Q2377=makeQuery(id+"F13.opPattern","COPY",BODY,{"derivedFrom":makeQuery(id+"F12.opPattern","COPY",BODY,{"derivedFrom":makeQuery(id+"F8.opPattern","COPY",BODY,{"derivedFrom":makeQuery(id+"F7.opPattern","COPY",BODY,{"derivedFrom":makeQuery(id+"F3.opPattern","COPY",BODY,{"derivedFrom":makeQuery(id+"F2.opPattern","COPY",BODY,{"derivedFrom":makeQuery(id+"F1.opRevolve","SWEPT_BODY",BODY,{"disambiguationData":[OSD([sQuery(id+"F0.wireOp",EDGE,"E1")])]}),"instanceName":"1"}),"instanceName":"1"}),"instanceName":"1"}),"instanceName":"1"}),"instanceName":"1"}),"instanceName":"1"});
            var Q2378;
            Q2378=makeQuery(id+"F13.opPattern","COPY",BODY,{"derivedFrom":makeQuery(id+"F12.opPattern","COPY",BODY,{"derivedFrom":makeQuery(id+"F8.opPattern","COPY",BODY,{"derivedFrom":makeQuery(id+"F7.opPattern","COPY",BODY,{"derivedFrom":makeQuery(id+"F4.opPattern","COPY",BODY,{"derivedFrom":makeQuery(id+"F1.opRevolve","SWEPT_BODY",BODY,{"disambiguationData":[OSD([sQuery(id+"F0.wireOp",EDGE,"E1")])]}),"instanceName":"1"}),"instanceName":"1"}),"instanceName":"1"}),"instanceName":"1"}),"instanceName":"1"});
            var Q2379;
            Q2379=makeQuery(id+"F13.opPattern","COPY",BODY,{"derivedFrom":makeQuery(id+"F12.opPattern","COPY",BODY,{"derivedFrom":makeQuery(id+"F8.opPattern","COPY",BODY,{"derivedFrom":makeQuery(id+"F7.opPattern","COPY",BODY,{"derivedFrom":makeQuery(id+"F4.opPattern","COPY",BODY,{"derivedFrom":makeQuery(id+"F2.opPattern","COPY",BODY,{"derivedFrom":makeQuery(id+"F1.opRevolve","SWEPT_BODY",BODY,{"disambiguationData":[OSD([sQuery(id+"F0.wireOp",EDGE,"E1")])]}),"instanceName":"1"}),"instanceName":"1"}),"instanceName":"1"}),"instanceName":"1"}),"instanceName":"1"}),"instanceName":"1"});
            var Q2380;
            Q2380=makeQuery(id+"F13.opPattern","COPY",BODY,{"derivedFrom":makeQuery(id+"F12.opPattern","COPY",BODY,{"derivedFrom":makeQuery(id+"F8.opPattern","COPY",BODY,{"derivedFrom":makeQuery(id+"F7.opPattern","COPY",BODY,{"derivedFrom":makeQuery(id+"F4.opPattern","COPY",BODY,{"derivedFrom":makeQuery(id+"F3.opPattern","COPY",BODY,{"derivedFrom":makeQuery(id+"F2.opPattern","COPY",BODY,{"derivedFrom":makeQuery(id+"F1.opRevolve","SWEPT_BODY",BODY,{"disambiguationData":[OSD([sQuery(id+"F0.wireOp",EDGE,"E1")])]}),"instanceName":"1"}),"instanceName":"1"}),"instanceName":"1"}),"instanceName":"1"}),"instanceName":"1"}),"instanceName":"1"}),"instanceName":"1"});
            var Q2381;
            Q2381=makeQuery(id+"F13.opPattern","COPY",BODY,{"derivedFrom":makeQuery(id+"F12.opPattern","COPY",BODY,{"derivedFrom":makeQuery(id+"F8.opPattern","COPY",BODY,{"derivedFrom":makeQuery(id+"F7.opPattern","COPY",BODY,{"derivedFrom":makeQuery(id+"F5.opPattern","COPY",BODY,{"derivedFrom":makeQuery(id+"F1.opRevolve","SWEPT_BODY",BODY,{"disambiguationData":[OSD([sQuery(id+"F0.wireOp",EDGE,"E1")])]}),"instanceName":"1"}),"instanceName":"1"}),"instanceName":"1"}),"instanceName":"1"}),"instanceName":"1"});
            var Q2382;
            Q2382=makeQuery(id+"F13.opPattern","COPY",BODY,{"derivedFrom":makeQuery(id+"F12.opPattern","COPY",BODY,{"derivedFrom":makeQuery(id+"F8.opPattern","COPY",BODY,{"derivedFrom":makeQuery(id+"F7.opPattern","COPY",BODY,{"derivedFrom":makeQuery(id+"F5.opPattern","COPY",BODY,{"derivedFrom":makeQuery(id+"F2.opPattern","COPY",BODY,{"derivedFrom":makeQuery(id+"F1.opRevolve","SWEPT_BODY",BODY,{"disambiguationData":[OSD([sQuery(id+"F0.wireOp",EDGE,"E1")])]}),"instanceName":"1"}),"instanceName":"1"}),"instanceName":"1"}),"instanceName":"1"}),"instanceName":"1"}),"instanceName":"1"});
            var Q2383;
            Q2383=makeQuery(id+"F13.opPattern","COPY",BODY,{"derivedFrom":makeQuery(id+"F12.opPattern","COPY",BODY,{"derivedFrom":makeQuery(id+"F8.opPattern","COPY",BODY,{"derivedFrom":makeQuery(id+"F7.opPattern","COPY",BODY,{"derivedFrom":makeQuery(id+"F5.opPattern","COPY",BODY,{"derivedFrom":makeQuery(id+"F3.opPattern","COPY",BODY,{"derivedFrom":makeQuery(id+"F2.opPattern","COPY",BODY,{"derivedFrom":makeQuery(id+"F1.opRevolve","SWEPT_BODY",BODY,{"disambiguationData":[OSD([sQuery(id+"F0.wireOp",EDGE,"E1")])]}),"instanceName":"1"}),"instanceName":"1"}),"instanceName":"1"}),"instanceName":"1"}),"instanceName":"1"}),"instanceName":"1"}),"instanceName":"1"});
            var Q2384;
            Q2384=makeQuery(id+"F13.opPattern","COPY",BODY,{"derivedFrom":makeQuery(id+"F12.opPattern","COPY",BODY,{"derivedFrom":makeQuery(id+"F8.opPattern","COPY",BODY,{"derivedFrom":makeQuery(id+"F7.opPattern","COPY",BODY,{"derivedFrom":makeQuery(id+"F5.opPattern","COPY",BODY,{"derivedFrom":makeQuery(id+"F4.opPattern","COPY",BODY,{"derivedFrom":makeQuery(id+"F1.opRevolve","SWEPT_BODY",BODY,{"disambiguationData":[OSD([sQuery(id+"F0.wireOp",EDGE,"E1")])]}),"instanceName":"1"}),"instanceName":"1"}),"instanceName":"1"}),"instanceName":"1"}),"instanceName":"1"}),"instanceName":"1"});
            var Q2385;
            Q2385=makeQuery(id+"F13.opPattern","COPY",BODY,{"derivedFrom":makeQuery(id+"F12.opPattern","COPY",BODY,{"derivedFrom":makeQuery(id+"F8.opPattern","COPY",BODY,{"derivedFrom":makeQuery(id+"F7.opPattern","COPY",BODY,{"derivedFrom":makeQuery(id+"F5.opPattern","COPY",BODY,{"derivedFrom":makeQuery(id+"F4.opPattern","COPY",BODY,{"derivedFrom":makeQuery(id+"F2.opPattern","COPY",BODY,{"derivedFrom":makeQuery(id+"F1.opRevolve","SWEPT_BODY",BODY,{"disambiguationData":[OSD([sQuery(id+"F0.wireOp",EDGE,"E1")])]}),"instanceName":"1"}),"instanceName":"1"}),"instanceName":"1"}),"instanceName":"1"}),"instanceName":"1"}),"instanceName":"1"}),"instanceName":"1"});
            var Q2386;
            Q2386=makeQuery(id+"F13.opPattern","COPY",BODY,{"derivedFrom":makeQuery(id+"F12.opPattern","COPY",BODY,{"derivedFrom":makeQuery(id+"F8.opPattern","COPY",BODY,{"derivedFrom":makeQuery(id+"F7.opPattern","COPY",BODY,{"derivedFrom":makeQuery(id+"F5.opPattern","COPY",BODY,{"derivedFrom":makeQuery(id+"F4.opPattern","COPY",BODY,{"derivedFrom":makeQuery(id+"F3.opPattern","COPY",BODY,{"derivedFrom":makeQuery(id+"F2.opPattern","COPY",BODY,{"derivedFrom":makeQuery(id+"F1.opRevolve","SWEPT_BODY",BODY,{"disambiguationData":[OSD([sQuery(id+"F0.wireOp",EDGE,"E1")])]}),"instanceName":"1"}),"instanceName":"1"}),"instanceName":"1"}),"instanceName":"1"}),"instanceName":"1"}),"instanceName":"1"}),"instanceName":"1"}),"instanceName":"1"});
            var Q2387;
            Q2387=makeQuery(id+"F13.opPattern","COPY",BODY,{"derivedFrom":makeQuery(id+"F12.opPattern","COPY",BODY,{"derivedFrom":makeQuery(id+"F8.opPattern","COPY",BODY,{"derivedFrom":makeQuery(id+"F7.opPattern","COPY",BODY,{"derivedFrom":makeQuery(id+"F6.opPattern","COPY",BODY,{"derivedFrom":makeQuery(id+"F1.opRevolve","SWEPT_BODY",BODY,{"disambiguationData":[OSD([sQuery(id+"F0.wireOp",EDGE,"E1")])]}),"instanceName":"1"}),"instanceName":"1"}),"instanceName":"1"}),"instanceName":"1"}),"instanceName":"1"});
            var Q2388;
            Q2388=makeQuery(id+"F13.opPattern","COPY",BODY,{"derivedFrom":makeQuery(id+"F12.opPattern","COPY",BODY,{"derivedFrom":makeQuery(id+"F8.opPattern","COPY",BODY,{"derivedFrom":makeQuery(id+"F7.opPattern","COPY",BODY,{"derivedFrom":makeQuery(id+"F6.opPattern","COPY",BODY,{"derivedFrom":makeQuery(id+"F2.opPattern","COPY",BODY,{"derivedFrom":makeQuery(id+"F1.opRevolve","SWEPT_BODY",BODY,{"disambiguationData":[OSD([sQuery(id+"F0.wireOp",EDGE,"E1")])]}),"instanceName":"1"}),"instanceName":"1"}),"instanceName":"1"}),"instanceName":"1"}),"instanceName":"1"}),"instanceName":"1"});
            var Q2389;
            Q2389=makeQuery(id+"F13.opPattern","COPY",BODY,{"derivedFrom":makeQuery(id+"F12.opPattern","COPY",BODY,{"derivedFrom":makeQuery(id+"F8.opPattern","COPY",BODY,{"derivedFrom":makeQuery(id+"F7.opPattern","COPY",BODY,{"derivedFrom":makeQuery(id+"F6.opPattern","COPY",BODY,{"derivedFrom":makeQuery(id+"F3.opPattern","COPY",BODY,{"derivedFrom":makeQuery(id+"F2.opPattern","COPY",BODY,{"derivedFrom":makeQuery(id+"F1.opRevolve","SWEPT_BODY",BODY,{"disambiguationData":[OSD([sQuery(id+"F0.wireOp",EDGE,"E1")])]}),"instanceName":"1"}),"instanceName":"1"}),"instanceName":"1"}),"instanceName":"1"}),"instanceName":"1"}),"instanceName":"1"}),"instanceName":"1"});
            var Q2390;
            Q2390=makeQuery(id+"F13.opPattern","COPY",BODY,{"derivedFrom":makeQuery(id+"F12.opPattern","COPY",BODY,{"derivedFrom":makeQuery(id+"F8.opPattern","COPY",BODY,{"derivedFrom":makeQuery(id+"F7.opPattern","COPY",BODY,{"derivedFrom":makeQuery(id+"F6.opPattern","COPY",BODY,{"derivedFrom":makeQuery(id+"F4.opPattern","COPY",BODY,{"derivedFrom":makeQuery(id+"F1.opRevolve","SWEPT_BODY",BODY,{"disambiguationData":[OSD([sQuery(id+"F0.wireOp",EDGE,"E1")])]}),"instanceName":"1"}),"instanceName":"1"}),"instanceName":"1"}),"instanceName":"1"}),"instanceName":"1"}),"instanceName":"1"});
            var Q2391;
            Q2391=makeQuery(id+"F13.opPattern","COPY",BODY,{"derivedFrom":makeQuery(id+"F12.opPattern","COPY",BODY,{"derivedFrom":makeQuery(id+"F8.opPattern","COPY",BODY,{"derivedFrom":makeQuery(id+"F7.opPattern","COPY",BODY,{"derivedFrom":makeQuery(id+"F6.opPattern","COPY",BODY,{"derivedFrom":makeQuery(id+"F4.opPattern","COPY",BODY,{"derivedFrom":makeQuery(id+"F2.opPattern","COPY",BODY,{"derivedFrom":makeQuery(id+"F1.opRevolve","SWEPT_BODY",BODY,{"disambiguationData":[OSD([sQuery(id+"F0.wireOp",EDGE,"E1")])]}),"instanceName":"1"}),"instanceName":"1"}),"instanceName":"1"}),"instanceName":"1"}),"instanceName":"1"}),"instanceName":"1"}),"instanceName":"1"});
            var Q2392;
            Q2392=makeQuery(id+"F13.opPattern","COPY",BODY,{"derivedFrom":makeQuery(id+"F12.opPattern","COPY",BODY,{"derivedFrom":makeQuery(id+"F8.opPattern","COPY",BODY,{"derivedFrom":makeQuery(id+"F7.opPattern","COPY",BODY,{"derivedFrom":makeQuery(id+"F6.opPattern","COPY",BODY,{"derivedFrom":makeQuery(id+"F4.opPattern","COPY",BODY,{"derivedFrom":makeQuery(id+"F3.opPattern","COPY",BODY,{"derivedFrom":makeQuery(id+"F2.opPattern","COPY",BODY,{"derivedFrom":makeQuery(id+"F1.opRevolve","SWEPT_BODY",BODY,{"disambiguationData":[OSD([sQuery(id+"F0.wireOp",EDGE,"E1")])]}),"instanceName":"1"}),"instanceName":"1"}),"instanceName":"1"}),"instanceName":"1"}),"instanceName":"1"}),"instanceName":"1"}),"instanceName":"1"}),"instanceName":"1"});
            var Q2393;
            Q2393=makeQuery(id+"F13.opPattern","COPY",BODY,{"derivedFrom":makeQuery(id+"F12.opPattern","COPY",BODY,{"derivedFrom":makeQuery(id+"F8.opPattern","COPY",BODY,{"derivedFrom":makeQuery(id+"F7.opPattern","COPY",BODY,{"derivedFrom":makeQuery(id+"F6.opPattern","COPY",BODY,{"derivedFrom":makeQuery(id+"F5.opPattern","COPY",BODY,{"derivedFrom":makeQuery(id+"F1.opRevolve","SWEPT_BODY",BODY,{"disambiguationData":[OSD([sQuery(id+"F0.wireOp",EDGE,"E1")])]}),"instanceName":"1"}),"instanceName":"1"}),"instanceName":"1"}),"instanceName":"1"}),"instanceName":"1"}),"instanceName":"1"});
            var Q2394;
            Q2394=makeQuery(id+"F13.opPattern","COPY",BODY,{"derivedFrom":makeQuery(id+"F12.opPattern","COPY",BODY,{"derivedFrom":makeQuery(id+"F8.opPattern","COPY",BODY,{"derivedFrom":makeQuery(id+"F7.opPattern","COPY",BODY,{"derivedFrom":makeQuery(id+"F6.opPattern","COPY",BODY,{"derivedFrom":makeQuery(id+"F5.opPattern","COPY",BODY,{"derivedFrom":makeQuery(id+"F2.opPattern","COPY",BODY,{"derivedFrom":makeQuery(id+"F1.opRevolve","SWEPT_BODY",BODY,{"disambiguationData":[OSD([sQuery(id+"F0.wireOp",EDGE,"E1")])]}),"instanceName":"1"}),"instanceName":"1"}),"instanceName":"1"}),"instanceName":"1"}),"instanceName":"1"}),"instanceName":"1"}),"instanceName":"1"});
            var Q2395;
            Q2395=makeQuery(id+"F13.opPattern","COPY",BODY,{"derivedFrom":makeQuery(id+"F12.opPattern","COPY",BODY,{"derivedFrom":makeQuery(id+"F8.opPattern","COPY",BODY,{"derivedFrom":makeQuery(id+"F7.opPattern","COPY",BODY,{"derivedFrom":makeQuery(id+"F6.opPattern","COPY",BODY,{"derivedFrom":makeQuery(id+"F5.opPattern","COPY",BODY,{"derivedFrom":makeQuery(id+"F3.opPattern","COPY",BODY,{"derivedFrom":makeQuery(id+"F2.opPattern","COPY",BODY,{"derivedFrom":makeQuery(id+"F1.opRevolve","SWEPT_BODY",BODY,{"disambiguationData":[OSD([sQuery(id+"F0.wireOp",EDGE,"E1")])]}),"instanceName":"1"}),"instanceName":"1"}),"instanceName":"1"}),"instanceName":"1"}),"instanceName":"1"}),"instanceName":"1"}),"instanceName":"1"}),"instanceName":"1"});
            var Q2396;
            Q2396=makeQuery(id+"F13.opPattern","COPY",BODY,{"derivedFrom":makeQuery(id+"F12.opPattern","COPY",BODY,{"derivedFrom":makeQuery(id+"F8.opPattern","COPY",BODY,{"derivedFrom":makeQuery(id+"F7.opPattern","COPY",BODY,{"derivedFrom":makeQuery(id+"F6.opPattern","COPY",BODY,{"derivedFrom":makeQuery(id+"F5.opPattern","COPY",BODY,{"derivedFrom":makeQuery(id+"F4.opPattern","COPY",BODY,{"derivedFrom":makeQuery(id+"F1.opRevolve","SWEPT_BODY",BODY,{"disambiguationData":[OSD([sQuery(id+"F0.wireOp",EDGE,"E1")])]}),"instanceName":"1"}),"instanceName":"1"}),"instanceName":"1"}),"instanceName":"1"}),"instanceName":"1"}),"instanceName":"1"}),"instanceName":"1"});
            var Q2397;
            Q2397=makeQuery(id+"F13.opPattern","COPY",BODY,{"derivedFrom":makeQuery(id+"F12.opPattern","COPY",BODY,{"derivedFrom":makeQuery(id+"F8.opPattern","COPY",BODY,{"derivedFrom":makeQuery(id+"F7.opPattern","COPY",BODY,{"derivedFrom":makeQuery(id+"F6.opPattern","COPY",BODY,{"derivedFrom":makeQuery(id+"F5.opPattern","COPY",BODY,{"derivedFrom":makeQuery(id+"F4.opPattern","COPY",BODY,{"derivedFrom":makeQuery(id+"F2.opPattern","COPY",BODY,{"derivedFrom":makeQuery(id+"F1.opRevolve","SWEPT_BODY",BODY,{"disambiguationData":[OSD([sQuery(id+"F0.wireOp",EDGE,"E1")])]}),"instanceName":"1"}),"instanceName":"1"}),"instanceName":"1"}),"instanceName":"1"}),"instanceName":"1"}),"instanceName":"1"}),"instanceName":"1"}),"instanceName":"1"});
            var Q2398;
            Q2398=makeQuery(id+"F13.opPattern","COPY",BODY,{"derivedFrom":makeQuery(id+"F12.opPattern","COPY",BODY,{"derivedFrom":makeQuery(id+"F8.opPattern","COPY",BODY,{"derivedFrom":makeQuery(id+"F7.opPattern","COPY",BODY,{"derivedFrom":makeQuery(id+"F6.opPattern","COPY",BODY,{"derivedFrom":makeQuery(id+"F5.opPattern","COPY",BODY,{"derivedFrom":makeQuery(id+"F4.opPattern","COPY",BODY,{"derivedFrom":makeQuery(id+"F3.opPattern","COPY",BODY,{"derivedFrom":makeQuery(id+"F2.opPattern","COPY",BODY,{"derivedFrom":makeQuery(id+"F1.opRevolve","SWEPT_BODY",BODY,{"disambiguationData":[OSD([sQuery(id+"F0.wireOp",EDGE,"E1")])]}),"instanceName":"1"}),"instanceName":"1"}),"instanceName":"1"}),"instanceName":"1"}),"instanceName":"1"}),"instanceName":"1"}),"instanceName":"1"}),"instanceName":"1"}),"instanceName":"1"});
            var Q2399;
            Q2399=makeQuery(id+"F13.opPattern","COPY",BODY,{"derivedFrom":makeQuery(id+"F12.opPattern","COPY",BODY,{"derivedFrom":makeQuery(id+"F9.opPattern","COPY",BODY,{"derivedFrom":makeQuery(id+"F1.opRevolve","SWEPT_BODY",BODY,{"disambiguationData":[OSD([sQuery(id+"F0.wireOp",EDGE,"E1")])]}),"instanceName":"1"}),"instanceName":"1"}),"instanceName":"1"});
            var Q2400;
            Q2400=makeQuery(id+"F13.opPattern","COPY",BODY,{"derivedFrom":makeQuery(id+"F12.opPattern","COPY",BODY,{"derivedFrom":makeQuery(id+"F9.opPattern","COPY",BODY,{"derivedFrom":makeQuery(id+"F2.opPattern","COPY",BODY,{"derivedFrom":makeQuery(id+"F1.opRevolve","SWEPT_BODY",BODY,{"disambiguationData":[OSD([sQuery(id+"F0.wireOp",EDGE,"E1")])]}),"instanceName":"1"}),"instanceName":"1"}),"instanceName":"1"}),"instanceName":"1"});
            var Q2401;
            Q2401=makeQuery(id+"F13.opPattern","COPY",BODY,{"derivedFrom":makeQuery(id+"F12.opPattern","COPY",BODY,{"derivedFrom":makeQuery(id+"F9.opPattern","COPY",BODY,{"derivedFrom":makeQuery(id+"F3.opPattern","COPY",BODY,{"derivedFrom":makeQuery(id+"F2.opPattern","COPY",BODY,{"derivedFrom":makeQuery(id+"F1.opRevolve","SWEPT_BODY",BODY,{"disambiguationData":[OSD([sQuery(id+"F0.wireOp",EDGE,"E1")])]}),"instanceName":"1"}),"instanceName":"1"}),"instanceName":"1"}),"instanceName":"1"}),"instanceName":"1"});
            var Q2402;
            Q2402=makeQuery(id+"F13.opPattern","COPY",BODY,{"derivedFrom":makeQuery(id+"F12.opPattern","COPY",BODY,{"derivedFrom":makeQuery(id+"F9.opPattern","COPY",BODY,{"derivedFrom":makeQuery(id+"F4.opPattern","COPY",BODY,{"derivedFrom":makeQuery(id+"F1.opRevolve","SWEPT_BODY",BODY,{"disambiguationData":[OSD([sQuery(id+"F0.wireOp",EDGE,"E1")])]}),"instanceName":"1"}),"instanceName":"1"}),"instanceName":"1"}),"instanceName":"1"});
            var Q2403;
            Q2403=makeQuery(id+"F13.opPattern","COPY",BODY,{"derivedFrom":makeQuery(id+"F12.opPattern","COPY",BODY,{"derivedFrom":makeQuery(id+"F9.opPattern","COPY",BODY,{"derivedFrom":makeQuery(id+"F4.opPattern","COPY",BODY,{"derivedFrom":makeQuery(id+"F2.opPattern","COPY",BODY,{"derivedFrom":makeQuery(id+"F1.opRevolve","SWEPT_BODY",BODY,{"disambiguationData":[OSD([sQuery(id+"F0.wireOp",EDGE,"E1")])]}),"instanceName":"1"}),"instanceName":"1"}),"instanceName":"1"}),"instanceName":"1"}),"instanceName":"1"});
            var Q2404;
            Q2404=makeQuery(id+"F13.opPattern","COPY",BODY,{"derivedFrom":makeQuery(id+"F12.opPattern","COPY",BODY,{"derivedFrom":makeQuery(id+"F9.opPattern","COPY",BODY,{"derivedFrom":makeQuery(id+"F4.opPattern","COPY",BODY,{"derivedFrom":makeQuery(id+"F3.opPattern","COPY",BODY,{"derivedFrom":makeQuery(id+"F2.opPattern","COPY",BODY,{"derivedFrom":makeQuery(id+"F1.opRevolve","SWEPT_BODY",BODY,{"disambiguationData":[OSD([sQuery(id+"F0.wireOp",EDGE,"E1")])]}),"instanceName":"1"}),"instanceName":"1"}),"instanceName":"1"}),"instanceName":"1"}),"instanceName":"1"}),"instanceName":"1"});
            var Q2405;
            Q2405=makeQuery(id+"F13.opPattern","COPY",BODY,{"derivedFrom":makeQuery(id+"F12.opPattern","COPY",BODY,{"derivedFrom":makeQuery(id+"F9.opPattern","COPY",BODY,{"derivedFrom":makeQuery(id+"F5.opPattern","COPY",BODY,{"derivedFrom":makeQuery(id+"F1.opRevolve","SWEPT_BODY",BODY,{"disambiguationData":[OSD([sQuery(id+"F0.wireOp",EDGE,"E1")])]}),"instanceName":"1"}),"instanceName":"1"}),"instanceName":"1"}),"instanceName":"1"});
            var Q2406;
            Q2406=makeQuery(id+"F13.opPattern","COPY",BODY,{"derivedFrom":makeQuery(id+"F12.opPattern","COPY",BODY,{"derivedFrom":makeQuery(id+"F9.opPattern","COPY",BODY,{"derivedFrom":makeQuery(id+"F5.opPattern","COPY",BODY,{"derivedFrom":makeQuery(id+"F2.opPattern","COPY",BODY,{"derivedFrom":makeQuery(id+"F1.opRevolve","SWEPT_BODY",BODY,{"disambiguationData":[OSD([sQuery(id+"F0.wireOp",EDGE,"E1")])]}),"instanceName":"1"}),"instanceName":"1"}),"instanceName":"1"}),"instanceName":"1"}),"instanceName":"1"});
            var Q2407;
            Q2407=makeQuery(id+"F13.opPattern","COPY",BODY,{"derivedFrom":makeQuery(id+"F12.opPattern","COPY",BODY,{"derivedFrom":makeQuery(id+"F9.opPattern","COPY",BODY,{"derivedFrom":makeQuery(id+"F5.opPattern","COPY",BODY,{"derivedFrom":makeQuery(id+"F3.opPattern","COPY",BODY,{"derivedFrom":makeQuery(id+"F2.opPattern","COPY",BODY,{"derivedFrom":makeQuery(id+"F1.opRevolve","SWEPT_BODY",BODY,{"disambiguationData":[OSD([sQuery(id+"F0.wireOp",EDGE,"E1")])]}),"instanceName":"1"}),"instanceName":"1"}),"instanceName":"1"}),"instanceName":"1"}),"instanceName":"1"}),"instanceName":"1"});
            var Q2408;
            Q2408=makeQuery(id+"F13.opPattern","COPY",BODY,{"derivedFrom":makeQuery(id+"F12.opPattern","COPY",BODY,{"derivedFrom":makeQuery(id+"F9.opPattern","COPY",BODY,{"derivedFrom":makeQuery(id+"F5.opPattern","COPY",BODY,{"derivedFrom":makeQuery(id+"F4.opPattern","COPY",BODY,{"derivedFrom":makeQuery(id+"F1.opRevolve","SWEPT_BODY",BODY,{"disambiguationData":[OSD([sQuery(id+"F0.wireOp",EDGE,"E1")])]}),"instanceName":"1"}),"instanceName":"1"}),"instanceName":"1"}),"instanceName":"1"}),"instanceName":"1"});
            var Q2409;
            Q2409=makeQuery(id+"F13.opPattern","COPY",BODY,{"derivedFrom":makeQuery(id+"F12.opPattern","COPY",BODY,{"derivedFrom":makeQuery(id+"F9.opPattern","COPY",BODY,{"derivedFrom":makeQuery(id+"F5.opPattern","COPY",BODY,{"derivedFrom":makeQuery(id+"F4.opPattern","COPY",BODY,{"derivedFrom":makeQuery(id+"F2.opPattern","COPY",BODY,{"derivedFrom":makeQuery(id+"F1.opRevolve","SWEPT_BODY",BODY,{"disambiguationData":[OSD([sQuery(id+"F0.wireOp",EDGE,"E1")])]}),"instanceName":"1"}),"instanceName":"1"}),"instanceName":"1"}),"instanceName":"1"}),"instanceName":"1"}),"instanceName":"1"});
            var Q2410;
            Q2410=makeQuery(id+"F13.opPattern","COPY",BODY,{"derivedFrom":makeQuery(id+"F12.opPattern","COPY",BODY,{"derivedFrom":makeQuery(id+"F9.opPattern","COPY",BODY,{"derivedFrom":makeQuery(id+"F5.opPattern","COPY",BODY,{"derivedFrom":makeQuery(id+"F4.opPattern","COPY",BODY,{"derivedFrom":makeQuery(id+"F3.opPattern","COPY",BODY,{"derivedFrom":makeQuery(id+"F2.opPattern","COPY",BODY,{"derivedFrom":makeQuery(id+"F1.opRevolve","SWEPT_BODY",BODY,{"disambiguationData":[OSD([sQuery(id+"F0.wireOp",EDGE,"E1")])]}),"instanceName":"1"}),"instanceName":"1"}),"instanceName":"1"}),"instanceName":"1"}),"instanceName":"1"}),"instanceName":"1"}),"instanceName":"1"});
            var Q2411;
            Q2411=makeQuery(id+"F13.opPattern","COPY",BODY,{"derivedFrom":makeQuery(id+"F12.opPattern","COPY",BODY,{"derivedFrom":makeQuery(id+"F9.opPattern","COPY",BODY,{"derivedFrom":makeQuery(id+"F6.opPattern","COPY",BODY,{"derivedFrom":makeQuery(id+"F1.opRevolve","SWEPT_BODY",BODY,{"disambiguationData":[OSD([sQuery(id+"F0.wireOp",EDGE,"E1")])]}),"instanceName":"1"}),"instanceName":"1"}),"instanceName":"1"}),"instanceName":"1"});
            var Q2412;
            Q2412=makeQuery(id+"F13.opPattern","COPY",BODY,{"derivedFrom":makeQuery(id+"F12.opPattern","COPY",BODY,{"derivedFrom":makeQuery(id+"F9.opPattern","COPY",BODY,{"derivedFrom":makeQuery(id+"F6.opPattern","COPY",BODY,{"derivedFrom":makeQuery(id+"F2.opPattern","COPY",BODY,{"derivedFrom":makeQuery(id+"F1.opRevolve","SWEPT_BODY",BODY,{"disambiguationData":[OSD([sQuery(id+"F0.wireOp",EDGE,"E1")])]}),"instanceName":"1"}),"instanceName":"1"}),"instanceName":"1"}),"instanceName":"1"}),"instanceName":"1"});
            var Q2413;
            Q2413=makeQuery(id+"F13.opPattern","COPY",BODY,{"derivedFrom":makeQuery(id+"F12.opPattern","COPY",BODY,{"derivedFrom":makeQuery(id+"F9.opPattern","COPY",BODY,{"derivedFrom":makeQuery(id+"F6.opPattern","COPY",BODY,{"derivedFrom":makeQuery(id+"F3.opPattern","COPY",BODY,{"derivedFrom":makeQuery(id+"F2.opPattern","COPY",BODY,{"derivedFrom":makeQuery(id+"F1.opRevolve","SWEPT_BODY",BODY,{"disambiguationData":[OSD([sQuery(id+"F0.wireOp",EDGE,"E1")])]}),"instanceName":"1"}),"instanceName":"1"}),"instanceName":"1"}),"instanceName":"1"}),"instanceName":"1"}),"instanceName":"1"});
            var Q2414;
            Q2414=makeQuery(id+"F13.opPattern","COPY",BODY,{"derivedFrom":makeQuery(id+"F12.opPattern","COPY",BODY,{"derivedFrom":makeQuery(id+"F9.opPattern","COPY",BODY,{"derivedFrom":makeQuery(id+"F6.opPattern","COPY",BODY,{"derivedFrom":makeQuery(id+"F4.opPattern","COPY",BODY,{"derivedFrom":makeQuery(id+"F1.opRevolve","SWEPT_BODY",BODY,{"disambiguationData":[OSD([sQuery(id+"F0.wireOp",EDGE,"E1")])]}),"instanceName":"1"}),"instanceName":"1"}),"instanceName":"1"}),"instanceName":"1"}),"instanceName":"1"});
            var Q2415;
            Q2415=makeQuery(id+"F13.opPattern","COPY",BODY,{"derivedFrom":makeQuery(id+"F12.opPattern","COPY",BODY,{"derivedFrom":makeQuery(id+"F9.opPattern","COPY",BODY,{"derivedFrom":makeQuery(id+"F6.opPattern","COPY",BODY,{"derivedFrom":makeQuery(id+"F4.opPattern","COPY",BODY,{"derivedFrom":makeQuery(id+"F2.opPattern","COPY",BODY,{"derivedFrom":makeQuery(id+"F1.opRevolve","SWEPT_BODY",BODY,{"disambiguationData":[OSD([sQuery(id+"F0.wireOp",EDGE,"E1")])]}),"instanceName":"1"}),"instanceName":"1"}),"instanceName":"1"}),"instanceName":"1"}),"instanceName":"1"}),"instanceName":"1"});
            var Q2416;
            Q2416=makeQuery(id+"F13.opPattern","COPY",BODY,{"derivedFrom":makeQuery(id+"F12.opPattern","COPY",BODY,{"derivedFrom":makeQuery(id+"F9.opPattern","COPY",BODY,{"derivedFrom":makeQuery(id+"F6.opPattern","COPY",BODY,{"derivedFrom":makeQuery(id+"F4.opPattern","COPY",BODY,{"derivedFrom":makeQuery(id+"F3.opPattern","COPY",BODY,{"derivedFrom":makeQuery(id+"F2.opPattern","COPY",BODY,{"derivedFrom":makeQuery(id+"F1.opRevolve","SWEPT_BODY",BODY,{"disambiguationData":[OSD([sQuery(id+"F0.wireOp",EDGE,"E1")])]}),"instanceName":"1"}),"instanceName":"1"}),"instanceName":"1"}),"instanceName":"1"}),"instanceName":"1"}),"instanceName":"1"}),"instanceName":"1"});
            var Q2417;
            Q2417=makeQuery(id+"F13.opPattern","COPY",BODY,{"derivedFrom":makeQuery(id+"F12.opPattern","COPY",BODY,{"derivedFrom":makeQuery(id+"F9.opPattern","COPY",BODY,{"derivedFrom":makeQuery(id+"F6.opPattern","COPY",BODY,{"derivedFrom":makeQuery(id+"F5.opPattern","COPY",BODY,{"derivedFrom":makeQuery(id+"F1.opRevolve","SWEPT_BODY",BODY,{"disambiguationData":[OSD([sQuery(id+"F0.wireOp",EDGE,"E1")])]}),"instanceName":"1"}),"instanceName":"1"}),"instanceName":"1"}),"instanceName":"1"}),"instanceName":"1"});
            var Q2418;
            Q2418=makeQuery(id+"F13.opPattern","COPY",BODY,{"derivedFrom":makeQuery(id+"F12.opPattern","COPY",BODY,{"derivedFrom":makeQuery(id+"F9.opPattern","COPY",BODY,{"derivedFrom":makeQuery(id+"F6.opPattern","COPY",BODY,{"derivedFrom":makeQuery(id+"F5.opPattern","COPY",BODY,{"derivedFrom":makeQuery(id+"F2.opPattern","COPY",BODY,{"derivedFrom":makeQuery(id+"F1.opRevolve","SWEPT_BODY",BODY,{"disambiguationData":[OSD([sQuery(id+"F0.wireOp",EDGE,"E1")])]}),"instanceName":"1"}),"instanceName":"1"}),"instanceName":"1"}),"instanceName":"1"}),"instanceName":"1"}),"instanceName":"1"});
            var Q2419;
            Q2419=makeQuery(id+"F13.opPattern","COPY",BODY,{"derivedFrom":makeQuery(id+"F12.opPattern","COPY",BODY,{"derivedFrom":makeQuery(id+"F9.opPattern","COPY",BODY,{"derivedFrom":makeQuery(id+"F6.opPattern","COPY",BODY,{"derivedFrom":makeQuery(id+"F5.opPattern","COPY",BODY,{"derivedFrom":makeQuery(id+"F3.opPattern","COPY",BODY,{"derivedFrom":makeQuery(id+"F2.opPattern","COPY",BODY,{"derivedFrom":makeQuery(id+"F1.opRevolve","SWEPT_BODY",BODY,{"disambiguationData":[OSD([sQuery(id+"F0.wireOp",EDGE,"E1")])]}),"instanceName":"1"}),"instanceName":"1"}),"instanceName":"1"}),"instanceName":"1"}),"instanceName":"1"}),"instanceName":"1"}),"instanceName":"1"});
            var Q2420;
            Q2420=makeQuery(id+"F13.opPattern","COPY",BODY,{"derivedFrom":makeQuery(id+"F12.opPattern","COPY",BODY,{"derivedFrom":makeQuery(id+"F9.opPattern","COPY",BODY,{"derivedFrom":makeQuery(id+"F6.opPattern","COPY",BODY,{"derivedFrom":makeQuery(id+"F5.opPattern","COPY",BODY,{"derivedFrom":makeQuery(id+"F4.opPattern","COPY",BODY,{"derivedFrom":makeQuery(id+"F1.opRevolve","SWEPT_BODY",BODY,{"disambiguationData":[OSD([sQuery(id+"F0.wireOp",EDGE,"E1")])]}),"instanceName":"1"}),"instanceName":"1"}),"instanceName":"1"}),"instanceName":"1"}),"instanceName":"1"}),"instanceName":"1"});
            var Q2421;
            Q2421=makeQuery(id+"F13.opPattern","COPY",BODY,{"derivedFrom":makeQuery(id+"F12.opPattern","COPY",BODY,{"derivedFrom":makeQuery(id+"F9.opPattern","COPY",BODY,{"derivedFrom":makeQuery(id+"F6.opPattern","COPY",BODY,{"derivedFrom":makeQuery(id+"F5.opPattern","COPY",BODY,{"derivedFrom":makeQuery(id+"F4.opPattern","COPY",BODY,{"derivedFrom":makeQuery(id+"F2.opPattern","COPY",BODY,{"derivedFrom":makeQuery(id+"F1.opRevolve","SWEPT_BODY",BODY,{"disambiguationData":[OSD([sQuery(id+"F0.wireOp",EDGE,"E1")])]}),"instanceName":"1"}),"instanceName":"1"}),"instanceName":"1"}),"instanceName":"1"}),"instanceName":"1"}),"instanceName":"1"}),"instanceName":"1"});
            var Q2422;
            Q2422=makeQuery(id+"F13.opPattern","COPY",BODY,{"derivedFrom":makeQuery(id+"F12.opPattern","COPY",BODY,{"derivedFrom":makeQuery(id+"F9.opPattern","COPY",BODY,{"derivedFrom":makeQuery(id+"F6.opPattern","COPY",BODY,{"derivedFrom":makeQuery(id+"F5.opPattern","COPY",BODY,{"derivedFrom":makeQuery(id+"F4.opPattern","COPY",BODY,{"derivedFrom":makeQuery(id+"F3.opPattern","COPY",BODY,{"derivedFrom":makeQuery(id+"F2.opPattern","COPY",BODY,{"derivedFrom":makeQuery(id+"F1.opRevolve","SWEPT_BODY",BODY,{"disambiguationData":[OSD([sQuery(id+"F0.wireOp",EDGE,"E1")])]}),"instanceName":"1"}),"instanceName":"1"}),"instanceName":"1"}),"instanceName":"1"}),"instanceName":"1"}),"instanceName":"1"}),"instanceName":"1"}),"instanceName":"1"});
            var Q2423;
            Q2423=makeQuery(id+"F13.opPattern","COPY",BODY,{"derivedFrom":makeQuery(id+"F12.opPattern","COPY",BODY,{"derivedFrom":makeQuery(id+"F9.opPattern","COPY",BODY,{"derivedFrom":makeQuery(id+"F7.opPattern","COPY",BODY,{"derivedFrom":makeQuery(id+"F1.opRevolve","SWEPT_BODY",BODY,{"disambiguationData":[OSD([sQuery(id+"F0.wireOp",EDGE,"E1")])]}),"instanceName":"1"}),"instanceName":"1"}),"instanceName":"1"}),"instanceName":"1"});
            var Q2424;
            Q2424=makeQuery(id+"F13.opPattern","COPY",BODY,{"derivedFrom":makeQuery(id+"F12.opPattern","COPY",BODY,{"derivedFrom":makeQuery(id+"F9.opPattern","COPY",BODY,{"derivedFrom":makeQuery(id+"F7.opPattern","COPY",BODY,{"derivedFrom":makeQuery(id+"F2.opPattern","COPY",BODY,{"derivedFrom":makeQuery(id+"F1.opRevolve","SWEPT_BODY",BODY,{"disambiguationData":[OSD([sQuery(id+"F0.wireOp",EDGE,"E1")])]}),"instanceName":"1"}),"instanceName":"1"}),"instanceName":"1"}),"instanceName":"1"}),"instanceName":"1"});
            var Q2425;
            Q2425=makeQuery(id+"F13.opPattern","COPY",BODY,{"derivedFrom":makeQuery(id+"F12.opPattern","COPY",BODY,{"derivedFrom":makeQuery(id+"F9.opPattern","COPY",BODY,{"derivedFrom":makeQuery(id+"F7.opPattern","COPY",BODY,{"derivedFrom":makeQuery(id+"F3.opPattern","COPY",BODY,{"derivedFrom":makeQuery(id+"F2.opPattern","COPY",BODY,{"derivedFrom":makeQuery(id+"F1.opRevolve","SWEPT_BODY",BODY,{"disambiguationData":[OSD([sQuery(id+"F0.wireOp",EDGE,"E1")])]}),"instanceName":"1"}),"instanceName":"1"}),"instanceName":"1"}),"instanceName":"1"}),"instanceName":"1"}),"instanceName":"1"});
            var Q2426;
            Q2426=makeQuery(id+"F13.opPattern","COPY",BODY,{"derivedFrom":makeQuery(id+"F12.opPattern","COPY",BODY,{"derivedFrom":makeQuery(id+"F9.opPattern","COPY",BODY,{"derivedFrom":makeQuery(id+"F7.opPattern","COPY",BODY,{"derivedFrom":makeQuery(id+"F4.opPattern","COPY",BODY,{"derivedFrom":makeQuery(id+"F1.opRevolve","SWEPT_BODY",BODY,{"disambiguationData":[OSD([sQuery(id+"F0.wireOp",EDGE,"E1")])]}),"instanceName":"1"}),"instanceName":"1"}),"instanceName":"1"}),"instanceName":"1"}),"instanceName":"1"});
            var Q2427;
            Q2427=makeQuery(id+"F13.opPattern","COPY",BODY,{"derivedFrom":makeQuery(id+"F12.opPattern","COPY",BODY,{"derivedFrom":makeQuery(id+"F9.opPattern","COPY",BODY,{"derivedFrom":makeQuery(id+"F7.opPattern","COPY",BODY,{"derivedFrom":makeQuery(id+"F4.opPattern","COPY",BODY,{"derivedFrom":makeQuery(id+"F2.opPattern","COPY",BODY,{"derivedFrom":makeQuery(id+"F1.opRevolve","SWEPT_BODY",BODY,{"disambiguationData":[OSD([sQuery(id+"F0.wireOp",EDGE,"E1")])]}),"instanceName":"1"}),"instanceName":"1"}),"instanceName":"1"}),"instanceName":"1"}),"instanceName":"1"}),"instanceName":"1"});
            var Q2428;
            Q2428=makeQuery(id+"F13.opPattern","COPY",BODY,{"derivedFrom":makeQuery(id+"F12.opPattern","COPY",BODY,{"derivedFrom":makeQuery(id+"F9.opPattern","COPY",BODY,{"derivedFrom":makeQuery(id+"F7.opPattern","COPY",BODY,{"derivedFrom":makeQuery(id+"F4.opPattern","COPY",BODY,{"derivedFrom":makeQuery(id+"F3.opPattern","COPY",BODY,{"derivedFrom":makeQuery(id+"F2.opPattern","COPY",BODY,{"derivedFrom":makeQuery(id+"F1.opRevolve","SWEPT_BODY",BODY,{"disambiguationData":[OSD([sQuery(id+"F0.wireOp",EDGE,"E1")])]}),"instanceName":"1"}),"instanceName":"1"}),"instanceName":"1"}),"instanceName":"1"}),"instanceName":"1"}),"instanceName":"1"}),"instanceName":"1"});
            var Q2429;
            Q2429=makeQuery(id+"F13.opPattern","COPY",BODY,{"derivedFrom":makeQuery(id+"F12.opPattern","COPY",BODY,{"derivedFrom":makeQuery(id+"F9.opPattern","COPY",BODY,{"derivedFrom":makeQuery(id+"F7.opPattern","COPY",BODY,{"derivedFrom":makeQuery(id+"F5.opPattern","COPY",BODY,{"derivedFrom":makeQuery(id+"F1.opRevolve","SWEPT_BODY",BODY,{"disambiguationData":[OSD([sQuery(id+"F0.wireOp",EDGE,"E1")])]}),"instanceName":"1"}),"instanceName":"1"}),"instanceName":"1"}),"instanceName":"1"}),"instanceName":"1"});
            var Q2430;
            Q2430=makeQuery(id+"F13.opPattern","COPY",BODY,{"derivedFrom":makeQuery(id+"F12.opPattern","COPY",BODY,{"derivedFrom":makeQuery(id+"F9.opPattern","COPY",BODY,{"derivedFrom":makeQuery(id+"F7.opPattern","COPY",BODY,{"derivedFrom":makeQuery(id+"F5.opPattern","COPY",BODY,{"derivedFrom":makeQuery(id+"F2.opPattern","COPY",BODY,{"derivedFrom":makeQuery(id+"F1.opRevolve","SWEPT_BODY",BODY,{"disambiguationData":[OSD([sQuery(id+"F0.wireOp",EDGE,"E1")])]}),"instanceName":"1"}),"instanceName":"1"}),"instanceName":"1"}),"instanceName":"1"}),"instanceName":"1"}),"instanceName":"1"});
            var Q2431;
            Q2431=makeQuery(id+"F13.opPattern","COPY",BODY,{"derivedFrom":makeQuery(id+"F12.opPattern","COPY",BODY,{"derivedFrom":makeQuery(id+"F9.opPattern","COPY",BODY,{"derivedFrom":makeQuery(id+"F7.opPattern","COPY",BODY,{"derivedFrom":makeQuery(id+"F5.opPattern","COPY",BODY,{"derivedFrom":makeQuery(id+"F3.opPattern","COPY",BODY,{"derivedFrom":makeQuery(id+"F2.opPattern","COPY",BODY,{"derivedFrom":makeQuery(id+"F1.opRevolve","SWEPT_BODY",BODY,{"disambiguationData":[OSD([sQuery(id+"F0.wireOp",EDGE,"E1")])]}),"instanceName":"1"}),"instanceName":"1"}),"instanceName":"1"}),"instanceName":"1"}),"instanceName":"1"}),"instanceName":"1"}),"instanceName":"1"});
            var Q2432;
            Q2432=makeQuery(id+"F13.opPattern","COPY",BODY,{"derivedFrom":makeQuery(id+"F12.opPattern","COPY",BODY,{"derivedFrom":makeQuery(id+"F9.opPattern","COPY",BODY,{"derivedFrom":makeQuery(id+"F7.opPattern","COPY",BODY,{"derivedFrom":makeQuery(id+"F5.opPattern","COPY",BODY,{"derivedFrom":makeQuery(id+"F4.opPattern","COPY",BODY,{"derivedFrom":makeQuery(id+"F1.opRevolve","SWEPT_BODY",BODY,{"disambiguationData":[OSD([sQuery(id+"F0.wireOp",EDGE,"E1")])]}),"instanceName":"1"}),"instanceName":"1"}),"instanceName":"1"}),"instanceName":"1"}),"instanceName":"1"}),"instanceName":"1"});
            var Q2433;
            Q2433=makeQuery(id+"F13.opPattern","COPY",BODY,{"derivedFrom":makeQuery(id+"F12.opPattern","COPY",BODY,{"derivedFrom":makeQuery(id+"F9.opPattern","COPY",BODY,{"derivedFrom":makeQuery(id+"F7.opPattern","COPY",BODY,{"derivedFrom":makeQuery(id+"F5.opPattern","COPY",BODY,{"derivedFrom":makeQuery(id+"F4.opPattern","COPY",BODY,{"derivedFrom":makeQuery(id+"F2.opPattern","COPY",BODY,{"derivedFrom":makeQuery(id+"F1.opRevolve","SWEPT_BODY",BODY,{"disambiguationData":[OSD([sQuery(id+"F0.wireOp",EDGE,"E1")])]}),"instanceName":"1"}),"instanceName":"1"}),"instanceName":"1"}),"instanceName":"1"}),"instanceName":"1"}),"instanceName":"1"}),"instanceName":"1"});
            var Q2434;
            Q2434=makeQuery(id+"F13.opPattern","COPY",BODY,{"derivedFrom":makeQuery(id+"F12.opPattern","COPY",BODY,{"derivedFrom":makeQuery(id+"F9.opPattern","COPY",BODY,{"derivedFrom":makeQuery(id+"F7.opPattern","COPY",BODY,{"derivedFrom":makeQuery(id+"F5.opPattern","COPY",BODY,{"derivedFrom":makeQuery(id+"F4.opPattern","COPY",BODY,{"derivedFrom":makeQuery(id+"F3.opPattern","COPY",BODY,{"derivedFrom":makeQuery(id+"F2.opPattern","COPY",BODY,{"derivedFrom":makeQuery(id+"F1.opRevolve","SWEPT_BODY",BODY,{"disambiguationData":[OSD([sQuery(id+"F0.wireOp",EDGE,"E1")])]}),"instanceName":"1"}),"instanceName":"1"}),"instanceName":"1"}),"instanceName":"1"}),"instanceName":"1"}),"instanceName":"1"}),"instanceName":"1"}),"instanceName":"1"});
            var Q2435;
            Q2435=makeQuery(id+"F13.opPattern","COPY",BODY,{"derivedFrom":makeQuery(id+"F12.opPattern","COPY",BODY,{"derivedFrom":makeQuery(id+"F9.opPattern","COPY",BODY,{"derivedFrom":makeQuery(id+"F7.opPattern","COPY",BODY,{"derivedFrom":makeQuery(id+"F6.opPattern","COPY",BODY,{"derivedFrom":makeQuery(id+"F1.opRevolve","SWEPT_BODY",BODY,{"disambiguationData":[OSD([sQuery(id+"F0.wireOp",EDGE,"E1")])]}),"instanceName":"1"}),"instanceName":"1"}),"instanceName":"1"}),"instanceName":"1"}),"instanceName":"1"});
            var Q2436;
            Q2436=makeQuery(id+"F13.opPattern","COPY",BODY,{"derivedFrom":makeQuery(id+"F12.opPattern","COPY",BODY,{"derivedFrom":makeQuery(id+"F9.opPattern","COPY",BODY,{"derivedFrom":makeQuery(id+"F7.opPattern","COPY",BODY,{"derivedFrom":makeQuery(id+"F6.opPattern","COPY",BODY,{"derivedFrom":makeQuery(id+"F2.opPattern","COPY",BODY,{"derivedFrom":makeQuery(id+"F1.opRevolve","SWEPT_BODY",BODY,{"disambiguationData":[OSD([sQuery(id+"F0.wireOp",EDGE,"E1")])]}),"instanceName":"1"}),"instanceName":"1"}),"instanceName":"1"}),"instanceName":"1"}),"instanceName":"1"}),"instanceName":"1"});
            var Q2437;
            Q2437=makeQuery(id+"F13.opPattern","COPY",BODY,{"derivedFrom":makeQuery(id+"F12.opPattern","COPY",BODY,{"derivedFrom":makeQuery(id+"F9.opPattern","COPY",BODY,{"derivedFrom":makeQuery(id+"F7.opPattern","COPY",BODY,{"derivedFrom":makeQuery(id+"F6.opPattern","COPY",BODY,{"derivedFrom":makeQuery(id+"F3.opPattern","COPY",BODY,{"derivedFrom":makeQuery(id+"F2.opPattern","COPY",BODY,{"derivedFrom":makeQuery(id+"F1.opRevolve","SWEPT_BODY",BODY,{"disambiguationData":[OSD([sQuery(id+"F0.wireOp",EDGE,"E1")])]}),"instanceName":"1"}),"instanceName":"1"}),"instanceName":"1"}),"instanceName":"1"}),"instanceName":"1"}),"instanceName":"1"}),"instanceName":"1"});
            var Q2438;
            Q2438=makeQuery(id+"F13.opPattern","COPY",BODY,{"derivedFrom":makeQuery(id+"F12.opPattern","COPY",BODY,{"derivedFrom":makeQuery(id+"F9.opPattern","COPY",BODY,{"derivedFrom":makeQuery(id+"F7.opPattern","COPY",BODY,{"derivedFrom":makeQuery(id+"F6.opPattern","COPY",BODY,{"derivedFrom":makeQuery(id+"F4.opPattern","COPY",BODY,{"derivedFrom":makeQuery(id+"F1.opRevolve","SWEPT_BODY",BODY,{"disambiguationData":[OSD([sQuery(id+"F0.wireOp",EDGE,"E1")])]}),"instanceName":"1"}),"instanceName":"1"}),"instanceName":"1"}),"instanceName":"1"}),"instanceName":"1"}),"instanceName":"1"});
            var Q2439;
            Q2439=makeQuery(id+"F13.opPattern","COPY",BODY,{"derivedFrom":makeQuery(id+"F12.opPattern","COPY",BODY,{"derivedFrom":makeQuery(id+"F9.opPattern","COPY",BODY,{"derivedFrom":makeQuery(id+"F7.opPattern","COPY",BODY,{"derivedFrom":makeQuery(id+"F6.opPattern","COPY",BODY,{"derivedFrom":makeQuery(id+"F4.opPattern","COPY",BODY,{"derivedFrom":makeQuery(id+"F2.opPattern","COPY",BODY,{"derivedFrom":makeQuery(id+"F1.opRevolve","SWEPT_BODY",BODY,{"disambiguationData":[OSD([sQuery(id+"F0.wireOp",EDGE,"E1")])]}),"instanceName":"1"}),"instanceName":"1"}),"instanceName":"1"}),"instanceName":"1"}),"instanceName":"1"}),"instanceName":"1"}),"instanceName":"1"});
            var Q2440;
            Q2440=makeQuery(id+"F13.opPattern","COPY",BODY,{"derivedFrom":makeQuery(id+"F12.opPattern","COPY",BODY,{"derivedFrom":makeQuery(id+"F9.opPattern","COPY",BODY,{"derivedFrom":makeQuery(id+"F7.opPattern","COPY",BODY,{"derivedFrom":makeQuery(id+"F6.opPattern","COPY",BODY,{"derivedFrom":makeQuery(id+"F4.opPattern","COPY",BODY,{"derivedFrom":makeQuery(id+"F3.opPattern","COPY",BODY,{"derivedFrom":makeQuery(id+"F2.opPattern","COPY",BODY,{"derivedFrom":makeQuery(id+"F1.opRevolve","SWEPT_BODY",BODY,{"disambiguationData":[OSD([sQuery(id+"F0.wireOp",EDGE,"E1")])]}),"instanceName":"1"}),"instanceName":"1"}),"instanceName":"1"}),"instanceName":"1"}),"instanceName":"1"}),"instanceName":"1"}),"instanceName":"1"}),"instanceName":"1"});
            var Q2441;
            Q2441=makeQuery(id+"F13.opPattern","COPY",BODY,{"derivedFrom":makeQuery(id+"F12.opPattern","COPY",BODY,{"derivedFrom":makeQuery(id+"F9.opPattern","COPY",BODY,{"derivedFrom":makeQuery(id+"F7.opPattern","COPY",BODY,{"derivedFrom":makeQuery(id+"F6.opPattern","COPY",BODY,{"derivedFrom":makeQuery(id+"F5.opPattern","COPY",BODY,{"derivedFrom":makeQuery(id+"F1.opRevolve","SWEPT_BODY",BODY,{"disambiguationData":[OSD([sQuery(id+"F0.wireOp",EDGE,"E1")])]}),"instanceName":"1"}),"instanceName":"1"}),"instanceName":"1"}),"instanceName":"1"}),"instanceName":"1"}),"instanceName":"1"});
            var Q2442;
            Q2442=makeQuery(id+"F13.opPattern","COPY",BODY,{"derivedFrom":makeQuery(id+"F12.opPattern","COPY",BODY,{"derivedFrom":makeQuery(id+"F9.opPattern","COPY",BODY,{"derivedFrom":makeQuery(id+"F7.opPattern","COPY",BODY,{"derivedFrom":makeQuery(id+"F6.opPattern","COPY",BODY,{"derivedFrom":makeQuery(id+"F5.opPattern","COPY",BODY,{"derivedFrom":makeQuery(id+"F2.opPattern","COPY",BODY,{"derivedFrom":makeQuery(id+"F1.opRevolve","SWEPT_BODY",BODY,{"disambiguationData":[OSD([sQuery(id+"F0.wireOp",EDGE,"E1")])]}),"instanceName":"1"}),"instanceName":"1"}),"instanceName":"1"}),"instanceName":"1"}),"instanceName":"1"}),"instanceName":"1"}),"instanceName":"1"});
            var Q2443;
            Q2443=makeQuery(id+"F13.opPattern","COPY",BODY,{"derivedFrom":makeQuery(id+"F12.opPattern","COPY",BODY,{"derivedFrom":makeQuery(id+"F9.opPattern","COPY",BODY,{"derivedFrom":makeQuery(id+"F7.opPattern","COPY",BODY,{"derivedFrom":makeQuery(id+"F6.opPattern","COPY",BODY,{"derivedFrom":makeQuery(id+"F5.opPattern","COPY",BODY,{"derivedFrom":makeQuery(id+"F3.opPattern","COPY",BODY,{"derivedFrom":makeQuery(id+"F2.opPattern","COPY",BODY,{"derivedFrom":makeQuery(id+"F1.opRevolve","SWEPT_BODY",BODY,{"disambiguationData":[OSD([sQuery(id+"F0.wireOp",EDGE,"E1")])]}),"instanceName":"1"}),"instanceName":"1"}),"instanceName":"1"}),"instanceName":"1"}),"instanceName":"1"}),"instanceName":"1"}),"instanceName":"1"}),"instanceName":"1"});
            var Q2444;
            Q2444=makeQuery(id+"F13.opPattern","COPY",BODY,{"derivedFrom":makeQuery(id+"F12.opPattern","COPY",BODY,{"derivedFrom":makeQuery(id+"F9.opPattern","COPY",BODY,{"derivedFrom":makeQuery(id+"F7.opPattern","COPY",BODY,{"derivedFrom":makeQuery(id+"F6.opPattern","COPY",BODY,{"derivedFrom":makeQuery(id+"F5.opPattern","COPY",BODY,{"derivedFrom":makeQuery(id+"F4.opPattern","COPY",BODY,{"derivedFrom":makeQuery(id+"F1.opRevolve","SWEPT_BODY",BODY,{"disambiguationData":[OSD([sQuery(id+"F0.wireOp",EDGE,"E1")])]}),"instanceName":"1"}),"instanceName":"1"}),"instanceName":"1"}),"instanceName":"1"}),"instanceName":"1"}),"instanceName":"1"}),"instanceName":"1"});
            var Q2445;
            Q2445=makeQuery(id+"F13.opPattern","COPY",BODY,{"derivedFrom":makeQuery(id+"F12.opPattern","COPY",BODY,{"derivedFrom":makeQuery(id+"F9.opPattern","COPY",BODY,{"derivedFrom":makeQuery(id+"F7.opPattern","COPY",BODY,{"derivedFrom":makeQuery(id+"F6.opPattern","COPY",BODY,{"derivedFrom":makeQuery(id+"F5.opPattern","COPY",BODY,{"derivedFrom":makeQuery(id+"F4.opPattern","COPY",BODY,{"derivedFrom":makeQuery(id+"F2.opPattern","COPY",BODY,{"derivedFrom":makeQuery(id+"F1.opRevolve","SWEPT_BODY",BODY,{"disambiguationData":[OSD([sQuery(id+"F0.wireOp",EDGE,"E1")])]}),"instanceName":"1"}),"instanceName":"1"}),"instanceName":"1"}),"instanceName":"1"}),"instanceName":"1"}),"instanceName":"1"}),"instanceName":"1"}),"instanceName":"1"});
            var Q2446;
            Q2446=makeQuery(id+"F13.opPattern","COPY",BODY,{"derivedFrom":makeQuery(id+"F12.opPattern","COPY",BODY,{"derivedFrom":makeQuery(id+"F9.opPattern","COPY",BODY,{"derivedFrom":makeQuery(id+"F7.opPattern","COPY",BODY,{"derivedFrom":makeQuery(id+"F6.opPattern","COPY",BODY,{"derivedFrom":makeQuery(id+"F5.opPattern","COPY",BODY,{"derivedFrom":makeQuery(id+"F4.opPattern","COPY",BODY,{"derivedFrom":makeQuery(id+"F3.opPattern","COPY",BODY,{"derivedFrom":makeQuery(id+"F2.opPattern","COPY",BODY,{"derivedFrom":makeQuery(id+"F1.opRevolve","SWEPT_BODY",BODY,{"disambiguationData":[OSD([sQuery(id+"F0.wireOp",EDGE,"E1")])]}),"instanceName":"1"}),"instanceName":"1"}),"instanceName":"1"}),"instanceName":"1"}),"instanceName":"1"}),"instanceName":"1"}),"instanceName":"1"}),"instanceName":"1"}),"instanceName":"1"});
            var Q2447;
            Q2447=makeQuery(id+"F13.opPattern","COPY",BODY,{"derivedFrom":makeQuery(id+"F12.opPattern","COPY",BODY,{"derivedFrom":makeQuery(id+"F9.opPattern","COPY",BODY,{"derivedFrom":makeQuery(id+"F8.opPattern","COPY",BODY,{"derivedFrom":makeQuery(id+"F1.opRevolve","SWEPT_BODY",BODY,{"disambiguationData":[OSD([sQuery(id+"F0.wireOp",EDGE,"E1")])]}),"instanceName":"1"}),"instanceName":"1"}),"instanceName":"1"}),"instanceName":"1"});
            var Q2448;
            Q2448=makeQuery(id+"F13.opPattern","COPY",BODY,{"derivedFrom":makeQuery(id+"F12.opPattern","COPY",BODY,{"derivedFrom":makeQuery(id+"F9.opPattern","COPY",BODY,{"derivedFrom":makeQuery(id+"F8.opPattern","COPY",BODY,{"derivedFrom":makeQuery(id+"F2.opPattern","COPY",BODY,{"derivedFrom":makeQuery(id+"F1.opRevolve","SWEPT_BODY",BODY,{"disambiguationData":[OSD([sQuery(id+"F0.wireOp",EDGE,"E1")])]}),"instanceName":"1"}),"instanceName":"1"}),"instanceName":"1"}),"instanceName":"1"}),"instanceName":"1"});
            var Q2449;
            Q2449=makeQuery(id+"F13.opPattern","COPY",BODY,{"derivedFrom":makeQuery(id+"F12.opPattern","COPY",BODY,{"derivedFrom":makeQuery(id+"F9.opPattern","COPY",BODY,{"derivedFrom":makeQuery(id+"F8.opPattern","COPY",BODY,{"derivedFrom":makeQuery(id+"F3.opPattern","COPY",BODY,{"derivedFrom":makeQuery(id+"F2.opPattern","COPY",BODY,{"derivedFrom":makeQuery(id+"F1.opRevolve","SWEPT_BODY",BODY,{"disambiguationData":[OSD([sQuery(id+"F0.wireOp",EDGE,"E1")])]}),"instanceName":"1"}),"instanceName":"1"}),"instanceName":"1"}),"instanceName":"1"}),"instanceName":"1"}),"instanceName":"1"});
            var Q2450;
            Q2450=makeQuery(id+"F13.opPattern","COPY",BODY,{"derivedFrom":makeQuery(id+"F12.opPattern","COPY",BODY,{"derivedFrom":makeQuery(id+"F9.opPattern","COPY",BODY,{"derivedFrom":makeQuery(id+"F8.opPattern","COPY",BODY,{"derivedFrom":makeQuery(id+"F4.opPattern","COPY",BODY,{"derivedFrom":makeQuery(id+"F1.opRevolve","SWEPT_BODY",BODY,{"disambiguationData":[OSD([sQuery(id+"F0.wireOp",EDGE,"E1")])]}),"instanceName":"1"}),"instanceName":"1"}),"instanceName":"1"}),"instanceName":"1"}),"instanceName":"1"});
            var Q2451;
            Q2451=makeQuery(id+"F13.opPattern","COPY",BODY,{"derivedFrom":makeQuery(id+"F12.opPattern","COPY",BODY,{"derivedFrom":makeQuery(id+"F9.opPattern","COPY",BODY,{"derivedFrom":makeQuery(id+"F8.opPattern","COPY",BODY,{"derivedFrom":makeQuery(id+"F4.opPattern","COPY",BODY,{"derivedFrom":makeQuery(id+"F2.opPattern","COPY",BODY,{"derivedFrom":makeQuery(id+"F1.opRevolve","SWEPT_BODY",BODY,{"disambiguationData":[OSD([sQuery(id+"F0.wireOp",EDGE,"E1")])]}),"instanceName":"1"}),"instanceName":"1"}),"instanceName":"1"}),"instanceName":"1"}),"instanceName":"1"}),"instanceName":"1"});
            var Q2452;
            Q2452=makeQuery(id+"F13.opPattern","COPY",BODY,{"derivedFrom":makeQuery(id+"F12.opPattern","COPY",BODY,{"derivedFrom":makeQuery(id+"F9.opPattern","COPY",BODY,{"derivedFrom":makeQuery(id+"F8.opPattern","COPY",BODY,{"derivedFrom":makeQuery(id+"F4.opPattern","COPY",BODY,{"derivedFrom":makeQuery(id+"F3.opPattern","COPY",BODY,{"derivedFrom":makeQuery(id+"F2.opPattern","COPY",BODY,{"derivedFrom":makeQuery(id+"F1.opRevolve","SWEPT_BODY",BODY,{"disambiguationData":[OSD([sQuery(id+"F0.wireOp",EDGE,"E1")])]}),"instanceName":"1"}),"instanceName":"1"}),"instanceName":"1"}),"instanceName":"1"}),"instanceName":"1"}),"instanceName":"1"}),"instanceName":"1"});
            var Q2453;
            Q2453=makeQuery(id+"F13.opPattern","COPY",BODY,{"derivedFrom":makeQuery(id+"F12.opPattern","COPY",BODY,{"derivedFrom":makeQuery(id+"F9.opPattern","COPY",BODY,{"derivedFrom":makeQuery(id+"F8.opPattern","COPY",BODY,{"derivedFrom":makeQuery(id+"F5.opPattern","COPY",BODY,{"derivedFrom":makeQuery(id+"F1.opRevolve","SWEPT_BODY",BODY,{"disambiguationData":[OSD([sQuery(id+"F0.wireOp",EDGE,"E1")])]}),"instanceName":"1"}),"instanceName":"1"}),"instanceName":"1"}),"instanceName":"1"}),"instanceName":"1"});
            var Q2454;
            Q2454=makeQuery(id+"F13.opPattern","COPY",BODY,{"derivedFrom":makeQuery(id+"F12.opPattern","COPY",BODY,{"derivedFrom":makeQuery(id+"F9.opPattern","COPY",BODY,{"derivedFrom":makeQuery(id+"F8.opPattern","COPY",BODY,{"derivedFrom":makeQuery(id+"F5.opPattern","COPY",BODY,{"derivedFrom":makeQuery(id+"F2.opPattern","COPY",BODY,{"derivedFrom":makeQuery(id+"F1.opRevolve","SWEPT_BODY",BODY,{"disambiguationData":[OSD([sQuery(id+"F0.wireOp",EDGE,"E1")])]}),"instanceName":"1"}),"instanceName":"1"}),"instanceName":"1"}),"instanceName":"1"}),"instanceName":"1"}),"instanceName":"1"});
            var Q2455;
            Q2455=makeQuery(id+"F13.opPattern","COPY",BODY,{"derivedFrom":makeQuery(id+"F12.opPattern","COPY",BODY,{"derivedFrom":makeQuery(id+"F9.opPattern","COPY",BODY,{"derivedFrom":makeQuery(id+"F8.opPattern","COPY",BODY,{"derivedFrom":makeQuery(id+"F5.opPattern","COPY",BODY,{"derivedFrom":makeQuery(id+"F3.opPattern","COPY",BODY,{"derivedFrom":makeQuery(id+"F2.opPattern","COPY",BODY,{"derivedFrom":makeQuery(id+"F1.opRevolve","SWEPT_BODY",BODY,{"disambiguationData":[OSD([sQuery(id+"F0.wireOp",EDGE,"E1")])]}),"instanceName":"1"}),"instanceName":"1"}),"instanceName":"1"}),"instanceName":"1"}),"instanceName":"1"}),"instanceName":"1"}),"instanceName":"1"});
            var Q2456;
            Q2456=makeQuery(id+"F13.opPattern","COPY",BODY,{"derivedFrom":makeQuery(id+"F12.opPattern","COPY",BODY,{"derivedFrom":makeQuery(id+"F9.opPattern","COPY",BODY,{"derivedFrom":makeQuery(id+"F8.opPattern","COPY",BODY,{"derivedFrom":makeQuery(id+"F5.opPattern","COPY",BODY,{"derivedFrom":makeQuery(id+"F4.opPattern","COPY",BODY,{"derivedFrom":makeQuery(id+"F1.opRevolve","SWEPT_BODY",BODY,{"disambiguationData":[OSD([sQuery(id+"F0.wireOp",EDGE,"E1")])]}),"instanceName":"1"}),"instanceName":"1"}),"instanceName":"1"}),"instanceName":"1"}),"instanceName":"1"}),"instanceName":"1"});
            var Q2457;
            Q2457=makeQuery(id+"F13.opPattern","COPY",BODY,{"derivedFrom":makeQuery(id+"F12.opPattern","COPY",BODY,{"derivedFrom":makeQuery(id+"F9.opPattern","COPY",BODY,{"derivedFrom":makeQuery(id+"F8.opPattern","COPY",BODY,{"derivedFrom":makeQuery(id+"F5.opPattern","COPY",BODY,{"derivedFrom":makeQuery(id+"F4.opPattern","COPY",BODY,{"derivedFrom":makeQuery(id+"F2.opPattern","COPY",BODY,{"derivedFrom":makeQuery(id+"F1.opRevolve","SWEPT_BODY",BODY,{"disambiguationData":[OSD([sQuery(id+"F0.wireOp",EDGE,"E1")])]}),"instanceName":"1"}),"instanceName":"1"}),"instanceName":"1"}),"instanceName":"1"}),"instanceName":"1"}),"instanceName":"1"}),"instanceName":"1"});
            var Q2458;
            Q2458=makeQuery(id+"F13.opPattern","COPY",BODY,{"derivedFrom":makeQuery(id+"F12.opPattern","COPY",BODY,{"derivedFrom":makeQuery(id+"F9.opPattern","COPY",BODY,{"derivedFrom":makeQuery(id+"F8.opPattern","COPY",BODY,{"derivedFrom":makeQuery(id+"F5.opPattern","COPY",BODY,{"derivedFrom":makeQuery(id+"F4.opPattern","COPY",BODY,{"derivedFrom":makeQuery(id+"F3.opPattern","COPY",BODY,{"derivedFrom":makeQuery(id+"F2.opPattern","COPY",BODY,{"derivedFrom":makeQuery(id+"F1.opRevolve","SWEPT_BODY",BODY,{"disambiguationData":[OSD([sQuery(id+"F0.wireOp",EDGE,"E1")])]}),"instanceName":"1"}),"instanceName":"1"}),"instanceName":"1"}),"instanceName":"1"}),"instanceName":"1"}),"instanceName":"1"}),"instanceName":"1"}),"instanceName":"1"});
            var Q2459;
            Q2459=makeQuery(id+"F13.opPattern","COPY",BODY,{"derivedFrom":makeQuery(id+"F12.opPattern","COPY",BODY,{"derivedFrom":makeQuery(id+"F9.opPattern","COPY",BODY,{"derivedFrom":makeQuery(id+"F8.opPattern","COPY",BODY,{"derivedFrom":makeQuery(id+"F6.opPattern","COPY",BODY,{"derivedFrom":makeQuery(id+"F1.opRevolve","SWEPT_BODY",BODY,{"disambiguationData":[OSD([sQuery(id+"F0.wireOp",EDGE,"E1")])]}),"instanceName":"1"}),"instanceName":"1"}),"instanceName":"1"}),"instanceName":"1"}),"instanceName":"1"});
            var Q2460;
            Q2460=makeQuery(id+"F13.opPattern","COPY",BODY,{"derivedFrom":makeQuery(id+"F12.opPattern","COPY",BODY,{"derivedFrom":makeQuery(id+"F9.opPattern","COPY",BODY,{"derivedFrom":makeQuery(id+"F8.opPattern","COPY",BODY,{"derivedFrom":makeQuery(id+"F6.opPattern","COPY",BODY,{"derivedFrom":makeQuery(id+"F2.opPattern","COPY",BODY,{"derivedFrom":makeQuery(id+"F1.opRevolve","SWEPT_BODY",BODY,{"disambiguationData":[OSD([sQuery(id+"F0.wireOp",EDGE,"E1")])]}),"instanceName":"1"}),"instanceName":"1"}),"instanceName":"1"}),"instanceName":"1"}),"instanceName":"1"}),"instanceName":"1"});
            var Q2461;
            Q2461=makeQuery(id+"F13.opPattern","COPY",BODY,{"derivedFrom":makeQuery(id+"F12.opPattern","COPY",BODY,{"derivedFrom":makeQuery(id+"F9.opPattern","COPY",BODY,{"derivedFrom":makeQuery(id+"F8.opPattern","COPY",BODY,{"derivedFrom":makeQuery(id+"F6.opPattern","COPY",BODY,{"derivedFrom":makeQuery(id+"F3.opPattern","COPY",BODY,{"derivedFrom":makeQuery(id+"F2.opPattern","COPY",BODY,{"derivedFrom":makeQuery(id+"F1.opRevolve","SWEPT_BODY",BODY,{"disambiguationData":[OSD([sQuery(id+"F0.wireOp",EDGE,"E1")])]}),"instanceName":"1"}),"instanceName":"1"}),"instanceName":"1"}),"instanceName":"1"}),"instanceName":"1"}),"instanceName":"1"}),"instanceName":"1"});
            var Q2462;
            Q2462=makeQuery(id+"F13.opPattern","COPY",BODY,{"derivedFrom":makeQuery(id+"F12.opPattern","COPY",BODY,{"derivedFrom":makeQuery(id+"F9.opPattern","COPY",BODY,{"derivedFrom":makeQuery(id+"F8.opPattern","COPY",BODY,{"derivedFrom":makeQuery(id+"F6.opPattern","COPY",BODY,{"derivedFrom":makeQuery(id+"F4.opPattern","COPY",BODY,{"derivedFrom":makeQuery(id+"F1.opRevolve","SWEPT_BODY",BODY,{"disambiguationData":[OSD([sQuery(id+"F0.wireOp",EDGE,"E1")])]}),"instanceName":"1"}),"instanceName":"1"}),"instanceName":"1"}),"instanceName":"1"}),"instanceName":"1"}),"instanceName":"1"});
            var Q2463;
            Q2463=makeQuery(id+"F13.opPattern","COPY",BODY,{"derivedFrom":makeQuery(id+"F12.opPattern","COPY",BODY,{"derivedFrom":makeQuery(id+"F9.opPattern","COPY",BODY,{"derivedFrom":makeQuery(id+"F8.opPattern","COPY",BODY,{"derivedFrom":makeQuery(id+"F6.opPattern","COPY",BODY,{"derivedFrom":makeQuery(id+"F4.opPattern","COPY",BODY,{"derivedFrom":makeQuery(id+"F2.opPattern","COPY",BODY,{"derivedFrom":makeQuery(id+"F1.opRevolve","SWEPT_BODY",BODY,{"disambiguationData":[OSD([sQuery(id+"F0.wireOp",EDGE,"E1")])]}),"instanceName":"1"}),"instanceName":"1"}),"instanceName":"1"}),"instanceName":"1"}),"instanceName":"1"}),"instanceName":"1"}),"instanceName":"1"});
            var Q2464;
            Q2464=makeQuery(id+"F13.opPattern","COPY",BODY,{"derivedFrom":makeQuery(id+"F12.opPattern","COPY",BODY,{"derivedFrom":makeQuery(id+"F9.opPattern","COPY",BODY,{"derivedFrom":makeQuery(id+"F8.opPattern","COPY",BODY,{"derivedFrom":makeQuery(id+"F6.opPattern","COPY",BODY,{"derivedFrom":makeQuery(id+"F4.opPattern","COPY",BODY,{"derivedFrom":makeQuery(id+"F3.opPattern","COPY",BODY,{"derivedFrom":makeQuery(id+"F2.opPattern","COPY",BODY,{"derivedFrom":makeQuery(id+"F1.opRevolve","SWEPT_BODY",BODY,{"disambiguationData":[OSD([sQuery(id+"F0.wireOp",EDGE,"E1")])]}),"instanceName":"1"}),"instanceName":"1"}),"instanceName":"1"}),"instanceName":"1"}),"instanceName":"1"}),"instanceName":"1"}),"instanceName":"1"}),"instanceName":"1"});
            var Q2465;
            Q2465=makeQuery(id+"F13.opPattern","COPY",BODY,{"derivedFrom":makeQuery(id+"F12.opPattern","COPY",BODY,{"derivedFrom":makeQuery(id+"F9.opPattern","COPY",BODY,{"derivedFrom":makeQuery(id+"F8.opPattern","COPY",BODY,{"derivedFrom":makeQuery(id+"F6.opPattern","COPY",BODY,{"derivedFrom":makeQuery(id+"F5.opPattern","COPY",BODY,{"derivedFrom":makeQuery(id+"F1.opRevolve","SWEPT_BODY",BODY,{"disambiguationData":[OSD([sQuery(id+"F0.wireOp",EDGE,"E1")])]}),"instanceName":"1"}),"instanceName":"1"}),"instanceName":"1"}),"instanceName":"1"}),"instanceName":"1"}),"instanceName":"1"});
            var Q2466;
            Q2466=makeQuery(id+"F13.opPattern","COPY",BODY,{"derivedFrom":makeQuery(id+"F12.opPattern","COPY",BODY,{"derivedFrom":makeQuery(id+"F9.opPattern","COPY",BODY,{"derivedFrom":makeQuery(id+"F8.opPattern","COPY",BODY,{"derivedFrom":makeQuery(id+"F6.opPattern","COPY",BODY,{"derivedFrom":makeQuery(id+"F5.opPattern","COPY",BODY,{"derivedFrom":makeQuery(id+"F2.opPattern","COPY",BODY,{"derivedFrom":makeQuery(id+"F1.opRevolve","SWEPT_BODY",BODY,{"disambiguationData":[OSD([sQuery(id+"F0.wireOp",EDGE,"E1")])]}),"instanceName":"1"}),"instanceName":"1"}),"instanceName":"1"}),"instanceName":"1"}),"instanceName":"1"}),"instanceName":"1"}),"instanceName":"1"});
            var Q2467;
            Q2467=makeQuery(id+"F13.opPattern","COPY",BODY,{"derivedFrom":makeQuery(id+"F12.opPattern","COPY",BODY,{"derivedFrom":makeQuery(id+"F9.opPattern","COPY",BODY,{"derivedFrom":makeQuery(id+"F8.opPattern","COPY",BODY,{"derivedFrom":makeQuery(id+"F6.opPattern","COPY",BODY,{"derivedFrom":makeQuery(id+"F5.opPattern","COPY",BODY,{"derivedFrom":makeQuery(id+"F3.opPattern","COPY",BODY,{"derivedFrom":makeQuery(id+"F2.opPattern","COPY",BODY,{"derivedFrom":makeQuery(id+"F1.opRevolve","SWEPT_BODY",BODY,{"disambiguationData":[OSD([sQuery(id+"F0.wireOp",EDGE,"E1")])]}),"instanceName":"1"}),"instanceName":"1"}),"instanceName":"1"}),"instanceName":"1"}),"instanceName":"1"}),"instanceName":"1"}),"instanceName":"1"}),"instanceName":"1"});
            var Q2468;
            Q2468=makeQuery(id+"F13.opPattern","COPY",BODY,{"derivedFrom":makeQuery(id+"F12.opPattern","COPY",BODY,{"derivedFrom":makeQuery(id+"F9.opPattern","COPY",BODY,{"derivedFrom":makeQuery(id+"F8.opPattern","COPY",BODY,{"derivedFrom":makeQuery(id+"F6.opPattern","COPY",BODY,{"derivedFrom":makeQuery(id+"F5.opPattern","COPY",BODY,{"derivedFrom":makeQuery(id+"F4.opPattern","COPY",BODY,{"derivedFrom":makeQuery(id+"F1.opRevolve","SWEPT_BODY",BODY,{"disambiguationData":[OSD([sQuery(id+"F0.wireOp",EDGE,"E1")])]}),"instanceName":"1"}),"instanceName":"1"}),"instanceName":"1"}),"instanceName":"1"}),"instanceName":"1"}),"instanceName":"1"}),"instanceName":"1"});
            var Q2469;
            Q2469=makeQuery(id+"F13.opPattern","COPY",BODY,{"derivedFrom":makeQuery(id+"F12.opPattern","COPY",BODY,{"derivedFrom":makeQuery(id+"F9.opPattern","COPY",BODY,{"derivedFrom":makeQuery(id+"F8.opPattern","COPY",BODY,{"derivedFrom":makeQuery(id+"F6.opPattern","COPY",BODY,{"derivedFrom":makeQuery(id+"F5.opPattern","COPY",BODY,{"derivedFrom":makeQuery(id+"F4.opPattern","COPY",BODY,{"derivedFrom":makeQuery(id+"F2.opPattern","COPY",BODY,{"derivedFrom":makeQuery(id+"F1.opRevolve","SWEPT_BODY",BODY,{"disambiguationData":[OSD([sQuery(id+"F0.wireOp",EDGE,"E1")])]}),"instanceName":"1"}),"instanceName":"1"}),"instanceName":"1"}),"instanceName":"1"}),"instanceName":"1"}),"instanceName":"1"}),"instanceName":"1"}),"instanceName":"1"});
            var Q2470;
            Q2470=makeQuery(id+"F13.opPattern","COPY",BODY,{"derivedFrom":makeQuery(id+"F12.opPattern","COPY",BODY,{"derivedFrom":makeQuery(id+"F9.opPattern","COPY",BODY,{"derivedFrom":makeQuery(id+"F8.opPattern","COPY",BODY,{"derivedFrom":makeQuery(id+"F6.opPattern","COPY",BODY,{"derivedFrom":makeQuery(id+"F5.opPattern","COPY",BODY,{"derivedFrom":makeQuery(id+"F4.opPattern","COPY",BODY,{"derivedFrom":makeQuery(id+"F3.opPattern","COPY",BODY,{"derivedFrom":makeQuery(id+"F2.opPattern","COPY",BODY,{"derivedFrom":makeQuery(id+"F1.opRevolve","SWEPT_BODY",BODY,{"disambiguationData":[OSD([sQuery(id+"F0.wireOp",EDGE,"E1")])]}),"instanceName":"1"}),"instanceName":"1"}),"instanceName":"1"}),"instanceName":"1"}),"instanceName":"1"}),"instanceName":"1"}),"instanceName":"1"}),"instanceName":"1"}),"instanceName":"1"});
            var Q2471;
            Q2471=makeQuery(id+"F13.opPattern","COPY",BODY,{"derivedFrom":makeQuery(id+"F12.opPattern","COPY",BODY,{"derivedFrom":makeQuery(id+"F9.opPattern","COPY",BODY,{"derivedFrom":makeQuery(id+"F8.opPattern","COPY",BODY,{"derivedFrom":makeQuery(id+"F7.opPattern","COPY",BODY,{"derivedFrom":makeQuery(id+"F1.opRevolve","SWEPT_BODY",BODY,{"disambiguationData":[OSD([sQuery(id+"F0.wireOp",EDGE,"E1")])]}),"instanceName":"1"}),"instanceName":"1"}),"instanceName":"1"}),"instanceName":"1"}),"instanceName":"1"});
            var Q2472;
            Q2472=makeQuery(id+"F13.opPattern","COPY",BODY,{"derivedFrom":makeQuery(id+"F12.opPattern","COPY",BODY,{"derivedFrom":makeQuery(id+"F9.opPattern","COPY",BODY,{"derivedFrom":makeQuery(id+"F8.opPattern","COPY",BODY,{"derivedFrom":makeQuery(id+"F7.opPattern","COPY",BODY,{"derivedFrom":makeQuery(id+"F2.opPattern","COPY",BODY,{"derivedFrom":makeQuery(id+"F1.opRevolve","SWEPT_BODY",BODY,{"disambiguationData":[OSD([sQuery(id+"F0.wireOp",EDGE,"E1")])]}),"instanceName":"1"}),"instanceName":"1"}),"instanceName":"1"}),"instanceName":"1"}),"instanceName":"1"}),"instanceName":"1"});
            var Q2473;
            Q2473=makeQuery(id+"F13.opPattern","COPY",BODY,{"derivedFrom":makeQuery(id+"F12.opPattern","COPY",BODY,{"derivedFrom":makeQuery(id+"F9.opPattern","COPY",BODY,{"derivedFrom":makeQuery(id+"F8.opPattern","COPY",BODY,{"derivedFrom":makeQuery(id+"F7.opPattern","COPY",BODY,{"derivedFrom":makeQuery(id+"F3.opPattern","COPY",BODY,{"derivedFrom":makeQuery(id+"F2.opPattern","COPY",BODY,{"derivedFrom":makeQuery(id+"F1.opRevolve","SWEPT_BODY",BODY,{"disambiguationData":[OSD([sQuery(id+"F0.wireOp",EDGE,"E1")])]}),"instanceName":"1"}),"instanceName":"1"}),"instanceName":"1"}),"instanceName":"1"}),"instanceName":"1"}),"instanceName":"1"}),"instanceName":"1"});
            var Q2474;
            Q2474=makeQuery(id+"F13.opPattern","COPY",BODY,{"derivedFrom":makeQuery(id+"F12.opPattern","COPY",BODY,{"derivedFrom":makeQuery(id+"F9.opPattern","COPY",BODY,{"derivedFrom":makeQuery(id+"F8.opPattern","COPY",BODY,{"derivedFrom":makeQuery(id+"F7.opPattern","COPY",BODY,{"derivedFrom":makeQuery(id+"F4.opPattern","COPY",BODY,{"derivedFrom":makeQuery(id+"F1.opRevolve","SWEPT_BODY",BODY,{"disambiguationData":[OSD([sQuery(id+"F0.wireOp",EDGE,"E1")])]}),"instanceName":"1"}),"instanceName":"1"}),"instanceName":"1"}),"instanceName":"1"}),"instanceName":"1"}),"instanceName":"1"});
            var Q2475;
            Q2475=makeQuery(id+"F13.opPattern","COPY",BODY,{"derivedFrom":makeQuery(id+"F12.opPattern","COPY",BODY,{"derivedFrom":makeQuery(id+"F9.opPattern","COPY",BODY,{"derivedFrom":makeQuery(id+"F8.opPattern","COPY",BODY,{"derivedFrom":makeQuery(id+"F7.opPattern","COPY",BODY,{"derivedFrom":makeQuery(id+"F4.opPattern","COPY",BODY,{"derivedFrom":makeQuery(id+"F2.opPattern","COPY",BODY,{"derivedFrom":makeQuery(id+"F1.opRevolve","SWEPT_BODY",BODY,{"disambiguationData":[OSD([sQuery(id+"F0.wireOp",EDGE,"E1")])]}),"instanceName":"1"}),"instanceName":"1"}),"instanceName":"1"}),"instanceName":"1"}),"instanceName":"1"}),"instanceName":"1"}),"instanceName":"1"});
            var Q2476;
            Q2476=makeQuery(id+"F13.opPattern","COPY",BODY,{"derivedFrom":makeQuery(id+"F12.opPattern","COPY",BODY,{"derivedFrom":makeQuery(id+"F9.opPattern","COPY",BODY,{"derivedFrom":makeQuery(id+"F8.opPattern","COPY",BODY,{"derivedFrom":makeQuery(id+"F7.opPattern","COPY",BODY,{"derivedFrom":makeQuery(id+"F4.opPattern","COPY",BODY,{"derivedFrom":makeQuery(id+"F3.opPattern","COPY",BODY,{"derivedFrom":makeQuery(id+"F2.opPattern","COPY",BODY,{"derivedFrom":makeQuery(id+"F1.opRevolve","SWEPT_BODY",BODY,{"disambiguationData":[OSD([sQuery(id+"F0.wireOp",EDGE,"E1")])]}),"instanceName":"1"}),"instanceName":"1"}),"instanceName":"1"}),"instanceName":"1"}),"instanceName":"1"}),"instanceName":"1"}),"instanceName":"1"}),"instanceName":"1"});
            var Q2477;
            Q2477=makeQuery(id+"F13.opPattern","COPY",BODY,{"derivedFrom":makeQuery(id+"F12.opPattern","COPY",BODY,{"derivedFrom":makeQuery(id+"F9.opPattern","COPY",BODY,{"derivedFrom":makeQuery(id+"F8.opPattern","COPY",BODY,{"derivedFrom":makeQuery(id+"F7.opPattern","COPY",BODY,{"derivedFrom":makeQuery(id+"F5.opPattern","COPY",BODY,{"derivedFrom":makeQuery(id+"F1.opRevolve","SWEPT_BODY",BODY,{"disambiguationData":[OSD([sQuery(id+"F0.wireOp",EDGE,"E1")])]}),"instanceName":"1"}),"instanceName":"1"}),"instanceName":"1"}),"instanceName":"1"}),"instanceName":"1"}),"instanceName":"1"});
            var Q2478;
            Q2478=makeQuery(id+"F13.opPattern","COPY",BODY,{"derivedFrom":makeQuery(id+"F12.opPattern","COPY",BODY,{"derivedFrom":makeQuery(id+"F9.opPattern","COPY",BODY,{"derivedFrom":makeQuery(id+"F8.opPattern","COPY",BODY,{"derivedFrom":makeQuery(id+"F7.opPattern","COPY",BODY,{"derivedFrom":makeQuery(id+"F5.opPattern","COPY",BODY,{"derivedFrom":makeQuery(id+"F2.opPattern","COPY",BODY,{"derivedFrom":makeQuery(id+"F1.opRevolve","SWEPT_BODY",BODY,{"disambiguationData":[OSD([sQuery(id+"F0.wireOp",EDGE,"E1")])]}),"instanceName":"1"}),"instanceName":"1"}),"instanceName":"1"}),"instanceName":"1"}),"instanceName":"1"}),"instanceName":"1"}),"instanceName":"1"});
            var Q2479;
            Q2479=makeQuery(id+"F13.opPattern","COPY",BODY,{"derivedFrom":makeQuery(id+"F12.opPattern","COPY",BODY,{"derivedFrom":makeQuery(id+"F9.opPattern","COPY",BODY,{"derivedFrom":makeQuery(id+"F8.opPattern","COPY",BODY,{"derivedFrom":makeQuery(id+"F7.opPattern","COPY",BODY,{"derivedFrom":makeQuery(id+"F5.opPattern","COPY",BODY,{"derivedFrom":makeQuery(id+"F3.opPattern","COPY",BODY,{"derivedFrom":makeQuery(id+"F2.opPattern","COPY",BODY,{"derivedFrom":makeQuery(id+"F1.opRevolve","SWEPT_BODY",BODY,{"disambiguationData":[OSD([sQuery(id+"F0.wireOp",EDGE,"E1")])]}),"instanceName":"1"}),"instanceName":"1"}),"instanceName":"1"}),"instanceName":"1"}),"instanceName":"1"}),"instanceName":"1"}),"instanceName":"1"}),"instanceName":"1"});
            var Q2480;
            Q2480=makeQuery(id+"F13.opPattern","COPY",BODY,{"derivedFrom":makeQuery(id+"F12.opPattern","COPY",BODY,{"derivedFrom":makeQuery(id+"F9.opPattern","COPY",BODY,{"derivedFrom":makeQuery(id+"F8.opPattern","COPY",BODY,{"derivedFrom":makeQuery(id+"F7.opPattern","COPY",BODY,{"derivedFrom":makeQuery(id+"F5.opPattern","COPY",BODY,{"derivedFrom":makeQuery(id+"F4.opPattern","COPY",BODY,{"derivedFrom":makeQuery(id+"F1.opRevolve","SWEPT_BODY",BODY,{"disambiguationData":[OSD([sQuery(id+"F0.wireOp",EDGE,"E1")])]}),"instanceName":"1"}),"instanceName":"1"}),"instanceName":"1"}),"instanceName":"1"}),"instanceName":"1"}),"instanceName":"1"}),"instanceName":"1"});
            var Q2481;
            Q2481=makeQuery(id+"F13.opPattern","COPY",BODY,{"derivedFrom":makeQuery(id+"F12.opPattern","COPY",BODY,{"derivedFrom":makeQuery(id+"F9.opPattern","COPY",BODY,{"derivedFrom":makeQuery(id+"F8.opPattern","COPY",BODY,{"derivedFrom":makeQuery(id+"F7.opPattern","COPY",BODY,{"derivedFrom":makeQuery(id+"F5.opPattern","COPY",BODY,{"derivedFrom":makeQuery(id+"F4.opPattern","COPY",BODY,{"derivedFrom":makeQuery(id+"F2.opPattern","COPY",BODY,{"derivedFrom":makeQuery(id+"F1.opRevolve","SWEPT_BODY",BODY,{"disambiguationData":[OSD([sQuery(id+"F0.wireOp",EDGE,"E1")])]}),"instanceName":"1"}),"instanceName":"1"}),"instanceName":"1"}),"instanceName":"1"}),"instanceName":"1"}),"instanceName":"1"}),"instanceName":"1"}),"instanceName":"1"});
            var Q2482;
            Q2482=makeQuery(id+"F13.opPattern","COPY",BODY,{"derivedFrom":makeQuery(id+"F12.opPattern","COPY",BODY,{"derivedFrom":makeQuery(id+"F9.opPattern","COPY",BODY,{"derivedFrom":makeQuery(id+"F8.opPattern","COPY",BODY,{"derivedFrom":makeQuery(id+"F7.opPattern","COPY",BODY,{"derivedFrom":makeQuery(id+"F5.opPattern","COPY",BODY,{"derivedFrom":makeQuery(id+"F4.opPattern","COPY",BODY,{"derivedFrom":makeQuery(id+"F3.opPattern","COPY",BODY,{"derivedFrom":makeQuery(id+"F2.opPattern","COPY",BODY,{"derivedFrom":makeQuery(id+"F1.opRevolve","SWEPT_BODY",BODY,{"disambiguationData":[OSD([sQuery(id+"F0.wireOp",EDGE,"E1")])]}),"instanceName":"1"}),"instanceName":"1"}),"instanceName":"1"}),"instanceName":"1"}),"instanceName":"1"}),"instanceName":"1"}),"instanceName":"1"}),"instanceName":"1"}),"instanceName":"1"});
            var Q2483;
            Q2483=makeQuery(id+"F13.opPattern","COPY",BODY,{"derivedFrom":makeQuery(id+"F12.opPattern","COPY",BODY,{"derivedFrom":makeQuery(id+"F9.opPattern","COPY",BODY,{"derivedFrom":makeQuery(id+"F8.opPattern","COPY",BODY,{"derivedFrom":makeQuery(id+"F7.opPattern","COPY",BODY,{"derivedFrom":makeQuery(id+"F6.opPattern","COPY",BODY,{"derivedFrom":makeQuery(id+"F1.opRevolve","SWEPT_BODY",BODY,{"disambiguationData":[OSD([sQuery(id+"F0.wireOp",EDGE,"E1")])]}),"instanceName":"1"}),"instanceName":"1"}),"instanceName":"1"}),"instanceName":"1"}),"instanceName":"1"}),"instanceName":"1"});
            var Q2484;
            Q2484=makeQuery(id+"F13.opPattern","COPY",BODY,{"derivedFrom":makeQuery(id+"F12.opPattern","COPY",BODY,{"derivedFrom":makeQuery(id+"F9.opPattern","COPY",BODY,{"derivedFrom":makeQuery(id+"F8.opPattern","COPY",BODY,{"derivedFrom":makeQuery(id+"F7.opPattern","COPY",BODY,{"derivedFrom":makeQuery(id+"F6.opPattern","COPY",BODY,{"derivedFrom":makeQuery(id+"F2.opPattern","COPY",BODY,{"derivedFrom":makeQuery(id+"F1.opRevolve","SWEPT_BODY",BODY,{"disambiguationData":[OSD([sQuery(id+"F0.wireOp",EDGE,"E1")])]}),"instanceName":"1"}),"instanceName":"1"}),"instanceName":"1"}),"instanceName":"1"}),"instanceName":"1"}),"instanceName":"1"}),"instanceName":"1"});
            var Q2485;
            Q2485=makeQuery(id+"F13.opPattern","COPY",BODY,{"derivedFrom":makeQuery(id+"F12.opPattern","COPY",BODY,{"derivedFrom":makeQuery(id+"F9.opPattern","COPY",BODY,{"derivedFrom":makeQuery(id+"F8.opPattern","COPY",BODY,{"derivedFrom":makeQuery(id+"F7.opPattern","COPY",BODY,{"derivedFrom":makeQuery(id+"F6.opPattern","COPY",BODY,{"derivedFrom":makeQuery(id+"F3.opPattern","COPY",BODY,{"derivedFrom":makeQuery(id+"F2.opPattern","COPY",BODY,{"derivedFrom":makeQuery(id+"F1.opRevolve","SWEPT_BODY",BODY,{"disambiguationData":[OSD([sQuery(id+"F0.wireOp",EDGE,"E1")])]}),"instanceName":"1"}),"instanceName":"1"}),"instanceName":"1"}),"instanceName":"1"}),"instanceName":"1"}),"instanceName":"1"}),"instanceName":"1"}),"instanceName":"1"});
            var Q2486;
            Q2486=makeQuery(id+"F13.opPattern","COPY",BODY,{"derivedFrom":makeQuery(id+"F12.opPattern","COPY",BODY,{"derivedFrom":makeQuery(id+"F9.opPattern","COPY",BODY,{"derivedFrom":makeQuery(id+"F8.opPattern","COPY",BODY,{"derivedFrom":makeQuery(id+"F7.opPattern","COPY",BODY,{"derivedFrom":makeQuery(id+"F6.opPattern","COPY",BODY,{"derivedFrom":makeQuery(id+"F4.opPattern","COPY",BODY,{"derivedFrom":makeQuery(id+"F1.opRevolve","SWEPT_BODY",BODY,{"disambiguationData":[OSD([sQuery(id+"F0.wireOp",EDGE,"E1")])]}),"instanceName":"1"}),"instanceName":"1"}),"instanceName":"1"}),"instanceName":"1"}),"instanceName":"1"}),"instanceName":"1"}),"instanceName":"1"});
            var Q2487;
            Q2487=makeQuery(id+"F13.opPattern","COPY",BODY,{"derivedFrom":makeQuery(id+"F12.opPattern","COPY",BODY,{"derivedFrom":makeQuery(id+"F9.opPattern","COPY",BODY,{"derivedFrom":makeQuery(id+"F8.opPattern","COPY",BODY,{"derivedFrom":makeQuery(id+"F7.opPattern","COPY",BODY,{"derivedFrom":makeQuery(id+"F6.opPattern","COPY",BODY,{"derivedFrom":makeQuery(id+"F4.opPattern","COPY",BODY,{"derivedFrom":makeQuery(id+"F2.opPattern","COPY",BODY,{"derivedFrom":makeQuery(id+"F1.opRevolve","SWEPT_BODY",BODY,{"disambiguationData":[OSD([sQuery(id+"F0.wireOp",EDGE,"E1")])]}),"instanceName":"1"}),"instanceName":"1"}),"instanceName":"1"}),"instanceName":"1"}),"instanceName":"1"}),"instanceName":"1"}),"instanceName":"1"}),"instanceName":"1"});
            var Q2488;
            Q2488=makeQuery(id+"F13.opPattern","COPY",BODY,{"derivedFrom":makeQuery(id+"F12.opPattern","COPY",BODY,{"derivedFrom":makeQuery(id+"F9.opPattern","COPY",BODY,{"derivedFrom":makeQuery(id+"F8.opPattern","COPY",BODY,{"derivedFrom":makeQuery(id+"F7.opPattern","COPY",BODY,{"derivedFrom":makeQuery(id+"F6.opPattern","COPY",BODY,{"derivedFrom":makeQuery(id+"F4.opPattern","COPY",BODY,{"derivedFrom":makeQuery(id+"F3.opPattern","COPY",BODY,{"derivedFrom":makeQuery(id+"F2.opPattern","COPY",BODY,{"derivedFrom":makeQuery(id+"F1.opRevolve","SWEPT_BODY",BODY,{"disambiguationData":[OSD([sQuery(id+"F0.wireOp",EDGE,"E1")])]}),"instanceName":"1"}),"instanceName":"1"}),"instanceName":"1"}),"instanceName":"1"}),"instanceName":"1"}),"instanceName":"1"}),"instanceName":"1"}),"instanceName":"1"}),"instanceName":"1"});
            var Q2489;
            Q2489=makeQuery(id+"F13.opPattern","COPY",BODY,{"derivedFrom":makeQuery(id+"F12.opPattern","COPY",BODY,{"derivedFrom":makeQuery(id+"F9.opPattern","COPY",BODY,{"derivedFrom":makeQuery(id+"F8.opPattern","COPY",BODY,{"derivedFrom":makeQuery(id+"F7.opPattern","COPY",BODY,{"derivedFrom":makeQuery(id+"F6.opPattern","COPY",BODY,{"derivedFrom":makeQuery(id+"F5.opPattern","COPY",BODY,{"derivedFrom":makeQuery(id+"F1.opRevolve","SWEPT_BODY",BODY,{"disambiguationData":[OSD([sQuery(id+"F0.wireOp",EDGE,"E1")])]}),"instanceName":"1"}),"instanceName":"1"}),"instanceName":"1"}),"instanceName":"1"}),"instanceName":"1"}),"instanceName":"1"}),"instanceName":"1"});
            var Q2490;
            Q2490=makeQuery(id+"F13.opPattern","COPY",BODY,{"derivedFrom":makeQuery(id+"F12.opPattern","COPY",BODY,{"derivedFrom":makeQuery(id+"F9.opPattern","COPY",BODY,{"derivedFrom":makeQuery(id+"F8.opPattern","COPY",BODY,{"derivedFrom":makeQuery(id+"F7.opPattern","COPY",BODY,{"derivedFrom":makeQuery(id+"F6.opPattern","COPY",BODY,{"derivedFrom":makeQuery(id+"F5.opPattern","COPY",BODY,{"derivedFrom":makeQuery(id+"F2.opPattern","COPY",BODY,{"derivedFrom":makeQuery(id+"F1.opRevolve","SWEPT_BODY",BODY,{"disambiguationData":[OSD([sQuery(id+"F0.wireOp",EDGE,"E1")])]}),"instanceName":"1"}),"instanceName":"1"}),"instanceName":"1"}),"instanceName":"1"}),"instanceName":"1"}),"instanceName":"1"}),"instanceName":"1"}),"instanceName":"1"});
            var Q2491;
            Q2491=makeQuery(id+"F13.opPattern","COPY",BODY,{"derivedFrom":makeQuery(id+"F12.opPattern","COPY",BODY,{"derivedFrom":makeQuery(id+"F9.opPattern","COPY",BODY,{"derivedFrom":makeQuery(id+"F8.opPattern","COPY",BODY,{"derivedFrom":makeQuery(id+"F7.opPattern","COPY",BODY,{"derivedFrom":makeQuery(id+"F6.opPattern","COPY",BODY,{"derivedFrom":makeQuery(id+"F5.opPattern","COPY",BODY,{"derivedFrom":makeQuery(id+"F3.opPattern","COPY",BODY,{"derivedFrom":makeQuery(id+"F2.opPattern","COPY",BODY,{"derivedFrom":makeQuery(id+"F1.opRevolve","SWEPT_BODY",BODY,{"disambiguationData":[OSD([sQuery(id+"F0.wireOp",EDGE,"E1")])]}),"instanceName":"1"}),"instanceName":"1"}),"instanceName":"1"}),"instanceName":"1"}),"instanceName":"1"}),"instanceName":"1"}),"instanceName":"1"}),"instanceName":"1"}),"instanceName":"1"});
            var Q2492;
            Q2492=makeQuery(id+"F13.opPattern","COPY",BODY,{"derivedFrom":makeQuery(id+"F12.opPattern","COPY",BODY,{"derivedFrom":makeQuery(id+"F9.opPattern","COPY",BODY,{"derivedFrom":makeQuery(id+"F8.opPattern","COPY",BODY,{"derivedFrom":makeQuery(id+"F7.opPattern","COPY",BODY,{"derivedFrom":makeQuery(id+"F6.opPattern","COPY",BODY,{"derivedFrom":makeQuery(id+"F5.opPattern","COPY",BODY,{"derivedFrom":makeQuery(id+"F4.opPattern","COPY",BODY,{"derivedFrom":makeQuery(id+"F1.opRevolve","SWEPT_BODY",BODY,{"disambiguationData":[OSD([sQuery(id+"F0.wireOp",EDGE,"E1")])]}),"instanceName":"1"}),"instanceName":"1"}),"instanceName":"1"}),"instanceName":"1"}),"instanceName":"1"}),"instanceName":"1"}),"instanceName":"1"}),"instanceName":"1"});
            var Q2493;
            Q2493=makeQuery(id+"F13.opPattern","COPY",BODY,{"derivedFrom":makeQuery(id+"F12.opPattern","COPY",BODY,{"derivedFrom":makeQuery(id+"F9.opPattern","COPY",BODY,{"derivedFrom":makeQuery(id+"F8.opPattern","COPY",BODY,{"derivedFrom":makeQuery(id+"F7.opPattern","COPY",BODY,{"derivedFrom":makeQuery(id+"F6.opPattern","COPY",BODY,{"derivedFrom":makeQuery(id+"F5.opPattern","COPY",BODY,{"derivedFrom":makeQuery(id+"F4.opPattern","COPY",BODY,{"derivedFrom":makeQuery(id+"F2.opPattern","COPY",BODY,{"derivedFrom":makeQuery(id+"F1.opRevolve","SWEPT_BODY",BODY,{"disambiguationData":[OSD([sQuery(id+"F0.wireOp",EDGE,"E1")])]}),"instanceName":"1"}),"instanceName":"1"}),"instanceName":"1"}),"instanceName":"1"}),"instanceName":"1"}),"instanceName":"1"}),"instanceName":"1"}),"instanceName":"1"}),"instanceName":"1"});
            var Q2494;
            Q2494=makeQuery(id+"F13.opPattern","COPY",BODY,{"derivedFrom":makeQuery(id+"F12.opPattern","COPY",BODY,{"derivedFrom":makeQuery(id+"F9.opPattern","COPY",BODY,{"derivedFrom":makeQuery(id+"F8.opPattern","COPY",BODY,{"derivedFrom":makeQuery(id+"F7.opPattern","COPY",BODY,{"derivedFrom":makeQuery(id+"F6.opPattern","COPY",BODY,{"derivedFrom":makeQuery(id+"F5.opPattern","COPY",BODY,{"derivedFrom":makeQuery(id+"F4.opPattern","COPY",BODY,{"derivedFrom":makeQuery(id+"F3.opPattern","COPY",BODY,{"derivedFrom":makeQuery(id+"F2.opPattern","COPY",BODY,{"derivedFrom":makeQuery(id+"F1.opRevolve","SWEPT_BODY",BODY,{"disambiguationData":[OSD([sQuery(id+"F0.wireOp",EDGE,"E1")])]}),"instanceName":"1"}),"instanceName":"1"}),"instanceName":"1"}),"instanceName":"1"}),"instanceName":"1"}),"instanceName":"1"}),"instanceName":"1"}),"instanceName":"1"}),"instanceName":"1"}),"instanceName":"1"});
            var Q2495;
            Q2495=makeQuery(id+"F13.opPattern","COPY",BODY,{"derivedFrom":makeQuery(id+"F12.opPattern","COPY",BODY,{"derivedFrom":makeQuery(id+"F10.opPattern","COPY",BODY,{"derivedFrom":makeQuery(id+"F1.opRevolve","SWEPT_BODY",BODY,{"disambiguationData":[OSD([sQuery(id+"F0.wireOp",EDGE,"E1")])]}),"instanceName":"1"}),"instanceName":"1"}),"instanceName":"1"});
            var Q2496;
            Q2496=makeQuery(id+"F13.opPattern","COPY",BODY,{"derivedFrom":makeQuery(id+"F12.opPattern","COPY",BODY,{"derivedFrom":makeQuery(id+"F10.opPattern","COPY",BODY,{"derivedFrom":makeQuery(id+"F2.opPattern","COPY",BODY,{"derivedFrom":makeQuery(id+"F1.opRevolve","SWEPT_BODY",BODY,{"disambiguationData":[OSD([sQuery(id+"F0.wireOp",EDGE,"E1")])]}),"instanceName":"1"}),"instanceName":"1"}),"instanceName":"1"}),"instanceName":"1"});
            var Q2497;
            Q2497=makeQuery(id+"F13.opPattern","COPY",BODY,{"derivedFrom":makeQuery(id+"F12.opPattern","COPY",BODY,{"derivedFrom":makeQuery(id+"F10.opPattern","COPY",BODY,{"derivedFrom":makeQuery(id+"F3.opPattern","COPY",BODY,{"derivedFrom":makeQuery(id+"F2.opPattern","COPY",BODY,{"derivedFrom":makeQuery(id+"F1.opRevolve","SWEPT_BODY",BODY,{"disambiguationData":[OSD([sQuery(id+"F0.wireOp",EDGE,"E1")])]}),"instanceName":"1"}),"instanceName":"1"}),"instanceName":"1"}),"instanceName":"1"}),"instanceName":"1"});
            var Q2498;
            Q2498=makeQuery(id+"F13.opPattern","COPY",BODY,{"derivedFrom":makeQuery(id+"F12.opPattern","COPY",BODY,{"derivedFrom":makeQuery(id+"F10.opPattern","COPY",BODY,{"derivedFrom":makeQuery(id+"F4.opPattern","COPY",BODY,{"derivedFrom":makeQuery(id+"F1.opRevolve","SWEPT_BODY",BODY,{"disambiguationData":[OSD([sQuery(id+"F0.wireOp",EDGE,"E1")])]}),"instanceName":"1"}),"instanceName":"1"}),"instanceName":"1"}),"instanceName":"1"});
            var Q2499;
            Q2499=makeQuery(id+"F13.opPattern","COPY",BODY,{"derivedFrom":makeQuery(id+"F12.opPattern","COPY",BODY,{"derivedFrom":makeQuery(id+"F10.opPattern","COPY",BODY,{"derivedFrom":makeQuery(id+"F4.opPattern","COPY",BODY,{"derivedFrom":makeQuery(id+"F2.opPattern","COPY",BODY,{"derivedFrom":makeQuery(id+"F1.opRevolve","SWEPT_BODY",BODY,{"disambiguationData":[OSD([sQuery(id+"F0.wireOp",EDGE,"E1")])]}),"instanceName":"1"}),"instanceName":"1"}),"instanceName":"1"}),"instanceName":"1"}),"instanceName":"1"});
            var Q2500;
            Q2500=makeQuery(id+"F13.opPattern","COPY",BODY,{"derivedFrom":makeQuery(id+"F12.opPattern","COPY",BODY,{"derivedFrom":makeQuery(id+"F10.opPattern","COPY",BODY,{"derivedFrom":makeQuery(id+"F4.opPattern","COPY",BODY,{"derivedFrom":makeQuery(id+"F3.opPattern","COPY",BODY,{"derivedFrom":makeQuery(id+"F2.opPattern","COPY",BODY,{"derivedFrom":makeQuery(id+"F1.opRevolve","SWEPT_BODY",BODY,{"disambiguationData":[OSD([sQuery(id+"F0.wireOp",EDGE,"E1")])]}),"instanceName":"1"}),"instanceName":"1"}),"instanceName":"1"}),"instanceName":"1"}),"instanceName":"1"}),"instanceName":"1"});
            var Q2501;
            Q2501=makeQuery(id+"F13.opPattern","COPY",BODY,{"derivedFrom":makeQuery(id+"F12.opPattern","COPY",BODY,{"derivedFrom":makeQuery(id+"F10.opPattern","COPY",BODY,{"derivedFrom":makeQuery(id+"F5.opPattern","COPY",BODY,{"derivedFrom":makeQuery(id+"F1.opRevolve","SWEPT_BODY",BODY,{"disambiguationData":[OSD([sQuery(id+"F0.wireOp",EDGE,"E1")])]}),"instanceName":"1"}),"instanceName":"1"}),"instanceName":"1"}),"instanceName":"1"});
            var Q2502;
            Q2502=makeQuery(id+"F13.opPattern","COPY",BODY,{"derivedFrom":makeQuery(id+"F12.opPattern","COPY",BODY,{"derivedFrom":makeQuery(id+"F10.opPattern","COPY",BODY,{"derivedFrom":makeQuery(id+"F5.opPattern","COPY",BODY,{"derivedFrom":makeQuery(id+"F2.opPattern","COPY",BODY,{"derivedFrom":makeQuery(id+"F1.opRevolve","SWEPT_BODY",BODY,{"disambiguationData":[OSD([sQuery(id+"F0.wireOp",EDGE,"E1")])]}),"instanceName":"1"}),"instanceName":"1"}),"instanceName":"1"}),"instanceName":"1"}),"instanceName":"1"});
            var Q2503;
            Q2503=makeQuery(id+"F13.opPattern","COPY",BODY,{"derivedFrom":makeQuery(id+"F12.opPattern","COPY",BODY,{"derivedFrom":makeQuery(id+"F10.opPattern","COPY",BODY,{"derivedFrom":makeQuery(id+"F5.opPattern","COPY",BODY,{"derivedFrom":makeQuery(id+"F3.opPattern","COPY",BODY,{"derivedFrom":makeQuery(id+"F2.opPattern","COPY",BODY,{"derivedFrom":makeQuery(id+"F1.opRevolve","SWEPT_BODY",BODY,{"disambiguationData":[OSD([sQuery(id+"F0.wireOp",EDGE,"E1")])]}),"instanceName":"1"}),"instanceName":"1"}),"instanceName":"1"}),"instanceName":"1"}),"instanceName":"1"}),"instanceName":"1"});
            var Q2504;
            Q2504=makeQuery(id+"F13.opPattern","COPY",BODY,{"derivedFrom":makeQuery(id+"F12.opPattern","COPY",BODY,{"derivedFrom":makeQuery(id+"F10.opPattern","COPY",BODY,{"derivedFrom":makeQuery(id+"F5.opPattern","COPY",BODY,{"derivedFrom":makeQuery(id+"F4.opPattern","COPY",BODY,{"derivedFrom":makeQuery(id+"F1.opRevolve","SWEPT_BODY",BODY,{"disambiguationData":[OSD([sQuery(id+"F0.wireOp",EDGE,"E1")])]}),"instanceName":"1"}),"instanceName":"1"}),"instanceName":"1"}),"instanceName":"1"}),"instanceName":"1"});
            var Q2505;
            Q2505=makeQuery(id+"F13.opPattern","COPY",BODY,{"derivedFrom":makeQuery(id+"F12.opPattern","COPY",BODY,{"derivedFrom":makeQuery(id+"F10.opPattern","COPY",BODY,{"derivedFrom":makeQuery(id+"F5.opPattern","COPY",BODY,{"derivedFrom":makeQuery(id+"F4.opPattern","COPY",BODY,{"derivedFrom":makeQuery(id+"F2.opPattern","COPY",BODY,{"derivedFrom":makeQuery(id+"F1.opRevolve","SWEPT_BODY",BODY,{"disambiguationData":[OSD([sQuery(id+"F0.wireOp",EDGE,"E1")])]}),"instanceName":"1"}),"instanceName":"1"}),"instanceName":"1"}),"instanceName":"1"}),"instanceName":"1"}),"instanceName":"1"});
            var Q2506;
            Q2506=makeQuery(id+"F13.opPattern","COPY",BODY,{"derivedFrom":makeQuery(id+"F12.opPattern","COPY",BODY,{"derivedFrom":makeQuery(id+"F10.opPattern","COPY",BODY,{"derivedFrom":makeQuery(id+"F5.opPattern","COPY",BODY,{"derivedFrom":makeQuery(id+"F4.opPattern","COPY",BODY,{"derivedFrom":makeQuery(id+"F3.opPattern","COPY",BODY,{"derivedFrom":makeQuery(id+"F2.opPattern","COPY",BODY,{"derivedFrom":makeQuery(id+"F1.opRevolve","SWEPT_BODY",BODY,{"disambiguationData":[OSD([sQuery(id+"F0.wireOp",EDGE,"E1")])]}),"instanceName":"1"}),"instanceName":"1"}),"instanceName":"1"}),"instanceName":"1"}),"instanceName":"1"}),"instanceName":"1"}),"instanceName":"1"});
            var Q2507;
            Q2507=makeQuery(id+"F13.opPattern","COPY",BODY,{"derivedFrom":makeQuery(id+"F12.opPattern","COPY",BODY,{"derivedFrom":makeQuery(id+"F10.opPattern","COPY",BODY,{"derivedFrom":makeQuery(id+"F6.opPattern","COPY",BODY,{"derivedFrom":makeQuery(id+"F1.opRevolve","SWEPT_BODY",BODY,{"disambiguationData":[OSD([sQuery(id+"F0.wireOp",EDGE,"E1")])]}),"instanceName":"1"}),"instanceName":"1"}),"instanceName":"1"}),"instanceName":"1"});
            var Q2508;
            Q2508=makeQuery(id+"F13.opPattern","COPY",BODY,{"derivedFrom":makeQuery(id+"F12.opPattern","COPY",BODY,{"derivedFrom":makeQuery(id+"F10.opPattern","COPY",BODY,{"derivedFrom":makeQuery(id+"F6.opPattern","COPY",BODY,{"derivedFrom":makeQuery(id+"F2.opPattern","COPY",BODY,{"derivedFrom":makeQuery(id+"F1.opRevolve","SWEPT_BODY",BODY,{"disambiguationData":[OSD([sQuery(id+"F0.wireOp",EDGE,"E1")])]}),"instanceName":"1"}),"instanceName":"1"}),"instanceName":"1"}),"instanceName":"1"}),"instanceName":"1"});
            var Q2509;
            Q2509=makeQuery(id+"F13.opPattern","COPY",BODY,{"derivedFrom":makeQuery(id+"F12.opPattern","COPY",BODY,{"derivedFrom":makeQuery(id+"F10.opPattern","COPY",BODY,{"derivedFrom":makeQuery(id+"F6.opPattern","COPY",BODY,{"derivedFrom":makeQuery(id+"F3.opPattern","COPY",BODY,{"derivedFrom":makeQuery(id+"F2.opPattern","COPY",BODY,{"derivedFrom":makeQuery(id+"F1.opRevolve","SWEPT_BODY",BODY,{"disambiguationData":[OSD([sQuery(id+"F0.wireOp",EDGE,"E1")])]}),"instanceName":"1"}),"instanceName":"1"}),"instanceName":"1"}),"instanceName":"1"}),"instanceName":"1"}),"instanceName":"1"});
            var Q2510;
            Q2510=makeQuery(id+"F13.opPattern","COPY",BODY,{"derivedFrom":makeQuery(id+"F12.opPattern","COPY",BODY,{"derivedFrom":makeQuery(id+"F10.opPattern","COPY",BODY,{"derivedFrom":makeQuery(id+"F6.opPattern","COPY",BODY,{"derivedFrom":makeQuery(id+"F4.opPattern","COPY",BODY,{"derivedFrom":makeQuery(id+"F1.opRevolve","SWEPT_BODY",BODY,{"disambiguationData":[OSD([sQuery(id+"F0.wireOp",EDGE,"E1")])]}),"instanceName":"1"}),"instanceName":"1"}),"instanceName":"1"}),"instanceName":"1"}),"instanceName":"1"});
            var Q2511;
            Q2511=makeQuery(id+"F13.opPattern","COPY",BODY,{"derivedFrom":makeQuery(id+"F12.opPattern","COPY",BODY,{"derivedFrom":makeQuery(id+"F10.opPattern","COPY",BODY,{"derivedFrom":makeQuery(id+"F6.opPattern","COPY",BODY,{"derivedFrom":makeQuery(id+"F4.opPattern","COPY",BODY,{"derivedFrom":makeQuery(id+"F2.opPattern","COPY",BODY,{"derivedFrom":makeQuery(id+"F1.opRevolve","SWEPT_BODY",BODY,{"disambiguationData":[OSD([sQuery(id+"F0.wireOp",EDGE,"E1")])]}),"instanceName":"1"}),"instanceName":"1"}),"instanceName":"1"}),"instanceName":"1"}),"instanceName":"1"}),"instanceName":"1"});
            var Q2512;
            Q2512=makeQuery(id+"F13.opPattern","COPY",BODY,{"derivedFrom":makeQuery(id+"F12.opPattern","COPY",BODY,{"derivedFrom":makeQuery(id+"F10.opPattern","COPY",BODY,{"derivedFrom":makeQuery(id+"F6.opPattern","COPY",BODY,{"derivedFrom":makeQuery(id+"F4.opPattern","COPY",BODY,{"derivedFrom":makeQuery(id+"F3.opPattern","COPY",BODY,{"derivedFrom":makeQuery(id+"F2.opPattern","COPY",BODY,{"derivedFrom":makeQuery(id+"F1.opRevolve","SWEPT_BODY",BODY,{"disambiguationData":[OSD([sQuery(id+"F0.wireOp",EDGE,"E1")])]}),"instanceName":"1"}),"instanceName":"1"}),"instanceName":"1"}),"instanceName":"1"}),"instanceName":"1"}),"instanceName":"1"}),"instanceName":"1"});
            var Q2513;
            Q2513=makeQuery(id+"F13.opPattern","COPY",BODY,{"derivedFrom":makeQuery(id+"F12.opPattern","COPY",BODY,{"derivedFrom":makeQuery(id+"F10.opPattern","COPY",BODY,{"derivedFrom":makeQuery(id+"F6.opPattern","COPY",BODY,{"derivedFrom":makeQuery(id+"F5.opPattern","COPY",BODY,{"derivedFrom":makeQuery(id+"F1.opRevolve","SWEPT_BODY",BODY,{"disambiguationData":[OSD([sQuery(id+"F0.wireOp",EDGE,"E1")])]}),"instanceName":"1"}),"instanceName":"1"}),"instanceName":"1"}),"instanceName":"1"}),"instanceName":"1"});
            var Q2514;
            Q2514=makeQuery(id+"F13.opPattern","COPY",BODY,{"derivedFrom":makeQuery(id+"F12.opPattern","COPY",BODY,{"derivedFrom":makeQuery(id+"F10.opPattern","COPY",BODY,{"derivedFrom":makeQuery(id+"F6.opPattern","COPY",BODY,{"derivedFrom":makeQuery(id+"F5.opPattern","COPY",BODY,{"derivedFrom":makeQuery(id+"F2.opPattern","COPY",BODY,{"derivedFrom":makeQuery(id+"F1.opRevolve","SWEPT_BODY",BODY,{"disambiguationData":[OSD([sQuery(id+"F0.wireOp",EDGE,"E1")])]}),"instanceName":"1"}),"instanceName":"1"}),"instanceName":"1"}),"instanceName":"1"}),"instanceName":"1"}),"instanceName":"1"});
            var Q2515;
            Q2515=makeQuery(id+"F13.opPattern","COPY",BODY,{"derivedFrom":makeQuery(id+"F12.opPattern","COPY",BODY,{"derivedFrom":makeQuery(id+"F10.opPattern","COPY",BODY,{"derivedFrom":makeQuery(id+"F6.opPattern","COPY",BODY,{"derivedFrom":makeQuery(id+"F5.opPattern","COPY",BODY,{"derivedFrom":makeQuery(id+"F3.opPattern","COPY",BODY,{"derivedFrom":makeQuery(id+"F2.opPattern","COPY",BODY,{"derivedFrom":makeQuery(id+"F1.opRevolve","SWEPT_BODY",BODY,{"disambiguationData":[OSD([sQuery(id+"F0.wireOp",EDGE,"E1")])]}),"instanceName":"1"}),"instanceName":"1"}),"instanceName":"1"}),"instanceName":"1"}),"instanceName":"1"}),"instanceName":"1"}),"instanceName":"1"});
            var Q2516;
            Q2516=makeQuery(id+"F13.opPattern","COPY",BODY,{"derivedFrom":makeQuery(id+"F12.opPattern","COPY",BODY,{"derivedFrom":makeQuery(id+"F10.opPattern","COPY",BODY,{"derivedFrom":makeQuery(id+"F6.opPattern","COPY",BODY,{"derivedFrom":makeQuery(id+"F5.opPattern","COPY",BODY,{"derivedFrom":makeQuery(id+"F4.opPattern","COPY",BODY,{"derivedFrom":makeQuery(id+"F1.opRevolve","SWEPT_BODY",BODY,{"disambiguationData":[OSD([sQuery(id+"F0.wireOp",EDGE,"E1")])]}),"instanceName":"1"}),"instanceName":"1"}),"instanceName":"1"}),"instanceName":"1"}),"instanceName":"1"}),"instanceName":"1"});
            var Q2517;
            Q2517=makeQuery(id+"F13.opPattern","COPY",BODY,{"derivedFrom":makeQuery(id+"F12.opPattern","COPY",BODY,{"derivedFrom":makeQuery(id+"F10.opPattern","COPY",BODY,{"derivedFrom":makeQuery(id+"F6.opPattern","COPY",BODY,{"derivedFrom":makeQuery(id+"F5.opPattern","COPY",BODY,{"derivedFrom":makeQuery(id+"F4.opPattern","COPY",BODY,{"derivedFrom":makeQuery(id+"F2.opPattern","COPY",BODY,{"derivedFrom":makeQuery(id+"F1.opRevolve","SWEPT_BODY",BODY,{"disambiguationData":[OSD([sQuery(id+"F0.wireOp",EDGE,"E1")])]}),"instanceName":"1"}),"instanceName":"1"}),"instanceName":"1"}),"instanceName":"1"}),"instanceName":"1"}),"instanceName":"1"}),"instanceName":"1"});
            var Q2518;
            Q2518=makeQuery(id+"F13.opPattern","COPY",BODY,{"derivedFrom":makeQuery(id+"F12.opPattern","COPY",BODY,{"derivedFrom":makeQuery(id+"F10.opPattern","COPY",BODY,{"derivedFrom":makeQuery(id+"F6.opPattern","COPY",BODY,{"derivedFrom":makeQuery(id+"F5.opPattern","COPY",BODY,{"derivedFrom":makeQuery(id+"F4.opPattern","COPY",BODY,{"derivedFrom":makeQuery(id+"F3.opPattern","COPY",BODY,{"derivedFrom":makeQuery(id+"F2.opPattern","COPY",BODY,{"derivedFrom":makeQuery(id+"F1.opRevolve","SWEPT_BODY",BODY,{"disambiguationData":[OSD([sQuery(id+"F0.wireOp",EDGE,"E1")])]}),"instanceName":"1"}),"instanceName":"1"}),"instanceName":"1"}),"instanceName":"1"}),"instanceName":"1"}),"instanceName":"1"}),"instanceName":"1"}),"instanceName":"1"});
            var Q2519;
            Q2519=makeQuery(id+"F13.opPattern","COPY",BODY,{"derivedFrom":makeQuery(id+"F12.opPattern","COPY",BODY,{"derivedFrom":makeQuery(id+"F10.opPattern","COPY",BODY,{"derivedFrom":makeQuery(id+"F7.opPattern","COPY",BODY,{"derivedFrom":makeQuery(id+"F1.opRevolve","SWEPT_BODY",BODY,{"disambiguationData":[OSD([sQuery(id+"F0.wireOp",EDGE,"E1")])]}),"instanceName":"1"}),"instanceName":"1"}),"instanceName":"1"}),"instanceName":"1"});
            var Q2520;
            Q2520=makeQuery(id+"F13.opPattern","COPY",BODY,{"derivedFrom":makeQuery(id+"F12.opPattern","COPY",BODY,{"derivedFrom":makeQuery(id+"F10.opPattern","COPY",BODY,{"derivedFrom":makeQuery(id+"F7.opPattern","COPY",BODY,{"derivedFrom":makeQuery(id+"F2.opPattern","COPY",BODY,{"derivedFrom":makeQuery(id+"F1.opRevolve","SWEPT_BODY",BODY,{"disambiguationData":[OSD([sQuery(id+"F0.wireOp",EDGE,"E1")])]}),"instanceName":"1"}),"instanceName":"1"}),"instanceName":"1"}),"instanceName":"1"}),"instanceName":"1"});
            var Q2521;
            Q2521=makeQuery(id+"F13.opPattern","COPY",BODY,{"derivedFrom":makeQuery(id+"F12.opPattern","COPY",BODY,{"derivedFrom":makeQuery(id+"F10.opPattern","COPY",BODY,{"derivedFrom":makeQuery(id+"F7.opPattern","COPY",BODY,{"derivedFrom":makeQuery(id+"F3.opPattern","COPY",BODY,{"derivedFrom":makeQuery(id+"F2.opPattern","COPY",BODY,{"derivedFrom":makeQuery(id+"F1.opRevolve","SWEPT_BODY",BODY,{"disambiguationData":[OSD([sQuery(id+"F0.wireOp",EDGE,"E1")])]}),"instanceName":"1"}),"instanceName":"1"}),"instanceName":"1"}),"instanceName":"1"}),"instanceName":"1"}),"instanceName":"1"});
            var Q2522;
            Q2522=makeQuery(id+"F13.opPattern","COPY",BODY,{"derivedFrom":makeQuery(id+"F12.opPattern","COPY",BODY,{"derivedFrom":makeQuery(id+"F10.opPattern","COPY",BODY,{"derivedFrom":makeQuery(id+"F7.opPattern","COPY",BODY,{"derivedFrom":makeQuery(id+"F4.opPattern","COPY",BODY,{"derivedFrom":makeQuery(id+"F1.opRevolve","SWEPT_BODY",BODY,{"disambiguationData":[OSD([sQuery(id+"F0.wireOp",EDGE,"E1")])]}),"instanceName":"1"}),"instanceName":"1"}),"instanceName":"1"}),"instanceName":"1"}),"instanceName":"1"});
            var Q2523;
            Q2523=makeQuery(id+"F13.opPattern","COPY",BODY,{"derivedFrom":makeQuery(id+"F12.opPattern","COPY",BODY,{"derivedFrom":makeQuery(id+"F10.opPattern","COPY",BODY,{"derivedFrom":makeQuery(id+"F7.opPattern","COPY",BODY,{"derivedFrom":makeQuery(id+"F4.opPattern","COPY",BODY,{"derivedFrom":makeQuery(id+"F2.opPattern","COPY",BODY,{"derivedFrom":makeQuery(id+"F1.opRevolve","SWEPT_BODY",BODY,{"disambiguationData":[OSD([sQuery(id+"F0.wireOp",EDGE,"E1")])]}),"instanceName":"1"}),"instanceName":"1"}),"instanceName":"1"}),"instanceName":"1"}),"instanceName":"1"}),"instanceName":"1"});
            var Q2524;
            Q2524=makeQuery(id+"F13.opPattern","COPY",BODY,{"derivedFrom":makeQuery(id+"F12.opPattern","COPY",BODY,{"derivedFrom":makeQuery(id+"F10.opPattern","COPY",BODY,{"derivedFrom":makeQuery(id+"F7.opPattern","COPY",BODY,{"derivedFrom":makeQuery(id+"F4.opPattern","COPY",BODY,{"derivedFrom":makeQuery(id+"F3.opPattern","COPY",BODY,{"derivedFrom":makeQuery(id+"F2.opPattern","COPY",BODY,{"derivedFrom":makeQuery(id+"F1.opRevolve","SWEPT_BODY",BODY,{"disambiguationData":[OSD([sQuery(id+"F0.wireOp",EDGE,"E1")])]}),"instanceName":"1"}),"instanceName":"1"}),"instanceName":"1"}),"instanceName":"1"}),"instanceName":"1"}),"instanceName":"1"}),"instanceName":"1"});
            var Q2525;
            Q2525=makeQuery(id+"F13.opPattern","COPY",BODY,{"derivedFrom":makeQuery(id+"F12.opPattern","COPY",BODY,{"derivedFrom":makeQuery(id+"F10.opPattern","COPY",BODY,{"derivedFrom":makeQuery(id+"F7.opPattern","COPY",BODY,{"derivedFrom":makeQuery(id+"F5.opPattern","COPY",BODY,{"derivedFrom":makeQuery(id+"F1.opRevolve","SWEPT_BODY",BODY,{"disambiguationData":[OSD([sQuery(id+"F0.wireOp",EDGE,"E1")])]}),"instanceName":"1"}),"instanceName":"1"}),"instanceName":"1"}),"instanceName":"1"}),"instanceName":"1"});
            var Q2526;
            Q2526=makeQuery(id+"F13.opPattern","COPY",BODY,{"derivedFrom":makeQuery(id+"F12.opPattern","COPY",BODY,{"derivedFrom":makeQuery(id+"F10.opPattern","COPY",BODY,{"derivedFrom":makeQuery(id+"F7.opPattern","COPY",BODY,{"derivedFrom":makeQuery(id+"F5.opPattern","COPY",BODY,{"derivedFrom":makeQuery(id+"F2.opPattern","COPY",BODY,{"derivedFrom":makeQuery(id+"F1.opRevolve","SWEPT_BODY",BODY,{"disambiguationData":[OSD([sQuery(id+"F0.wireOp",EDGE,"E1")])]}),"instanceName":"1"}),"instanceName":"1"}),"instanceName":"1"}),"instanceName":"1"}),"instanceName":"1"}),"instanceName":"1"});
            var Q2527;
            Q2527=makeQuery(id+"F13.opPattern","COPY",BODY,{"derivedFrom":makeQuery(id+"F12.opPattern","COPY",BODY,{"derivedFrom":makeQuery(id+"F10.opPattern","COPY",BODY,{"derivedFrom":makeQuery(id+"F7.opPattern","COPY",BODY,{"derivedFrom":makeQuery(id+"F5.opPattern","COPY",BODY,{"derivedFrom":makeQuery(id+"F3.opPattern","COPY",BODY,{"derivedFrom":makeQuery(id+"F2.opPattern","COPY",BODY,{"derivedFrom":makeQuery(id+"F1.opRevolve","SWEPT_BODY",BODY,{"disambiguationData":[OSD([sQuery(id+"F0.wireOp",EDGE,"E1")])]}),"instanceName":"1"}),"instanceName":"1"}),"instanceName":"1"}),"instanceName":"1"}),"instanceName":"1"}),"instanceName":"1"}),"instanceName":"1"});
            var Q2528;
            Q2528=makeQuery(id+"F13.opPattern","COPY",BODY,{"derivedFrom":makeQuery(id+"F12.opPattern","COPY",BODY,{"derivedFrom":makeQuery(id+"F10.opPattern","COPY",BODY,{"derivedFrom":makeQuery(id+"F7.opPattern","COPY",BODY,{"derivedFrom":makeQuery(id+"F5.opPattern","COPY",BODY,{"derivedFrom":makeQuery(id+"F4.opPattern","COPY",BODY,{"derivedFrom":makeQuery(id+"F1.opRevolve","SWEPT_BODY",BODY,{"disambiguationData":[OSD([sQuery(id+"F0.wireOp",EDGE,"E1")])]}),"instanceName":"1"}),"instanceName":"1"}),"instanceName":"1"}),"instanceName":"1"}),"instanceName":"1"}),"instanceName":"1"});
            var Q2529;
            Q2529=makeQuery(id+"F13.opPattern","COPY",BODY,{"derivedFrom":makeQuery(id+"F12.opPattern","COPY",BODY,{"derivedFrom":makeQuery(id+"F10.opPattern","COPY",BODY,{"derivedFrom":makeQuery(id+"F7.opPattern","COPY",BODY,{"derivedFrom":makeQuery(id+"F5.opPattern","COPY",BODY,{"derivedFrom":makeQuery(id+"F4.opPattern","COPY",BODY,{"derivedFrom":makeQuery(id+"F2.opPattern","COPY",BODY,{"derivedFrom":makeQuery(id+"F1.opRevolve","SWEPT_BODY",BODY,{"disambiguationData":[OSD([sQuery(id+"F0.wireOp",EDGE,"E1")])]}),"instanceName":"1"}),"instanceName":"1"}),"instanceName":"1"}),"instanceName":"1"}),"instanceName":"1"}),"instanceName":"1"}),"instanceName":"1"});
            var Q2530;
            Q2530=makeQuery(id+"F13.opPattern","COPY",BODY,{"derivedFrom":makeQuery(id+"F12.opPattern","COPY",BODY,{"derivedFrom":makeQuery(id+"F10.opPattern","COPY",BODY,{"derivedFrom":makeQuery(id+"F7.opPattern","COPY",BODY,{"derivedFrom":makeQuery(id+"F5.opPattern","COPY",BODY,{"derivedFrom":makeQuery(id+"F4.opPattern","COPY",BODY,{"derivedFrom":makeQuery(id+"F3.opPattern","COPY",BODY,{"derivedFrom":makeQuery(id+"F2.opPattern","COPY",BODY,{"derivedFrom":makeQuery(id+"F1.opRevolve","SWEPT_BODY",BODY,{"disambiguationData":[OSD([sQuery(id+"F0.wireOp",EDGE,"E1")])]}),"instanceName":"1"}),"instanceName":"1"}),"instanceName":"1"}),"instanceName":"1"}),"instanceName":"1"}),"instanceName":"1"}),"instanceName":"1"}),"instanceName":"1"});
            var Q2531;
            Q2531=makeQuery(id+"F13.opPattern","COPY",BODY,{"derivedFrom":makeQuery(id+"F12.opPattern","COPY",BODY,{"derivedFrom":makeQuery(id+"F10.opPattern","COPY",BODY,{"derivedFrom":makeQuery(id+"F7.opPattern","COPY",BODY,{"derivedFrom":makeQuery(id+"F6.opPattern","COPY",BODY,{"derivedFrom":makeQuery(id+"F1.opRevolve","SWEPT_BODY",BODY,{"disambiguationData":[OSD([sQuery(id+"F0.wireOp",EDGE,"E1")])]}),"instanceName":"1"}),"instanceName":"1"}),"instanceName":"1"}),"instanceName":"1"}),"instanceName":"1"});
            var Q2532;
            Q2532=makeQuery(id+"F13.opPattern","COPY",BODY,{"derivedFrom":makeQuery(id+"F12.opPattern","COPY",BODY,{"derivedFrom":makeQuery(id+"F10.opPattern","COPY",BODY,{"derivedFrom":makeQuery(id+"F7.opPattern","COPY",BODY,{"derivedFrom":makeQuery(id+"F6.opPattern","COPY",BODY,{"derivedFrom":makeQuery(id+"F2.opPattern","COPY",BODY,{"derivedFrom":makeQuery(id+"F1.opRevolve","SWEPT_BODY",BODY,{"disambiguationData":[OSD([sQuery(id+"F0.wireOp",EDGE,"E1")])]}),"instanceName":"1"}),"instanceName":"1"}),"instanceName":"1"}),"instanceName":"1"}),"instanceName":"1"}),"instanceName":"1"});
            var Q2533;
            Q2533=makeQuery(id+"F13.opPattern","COPY",BODY,{"derivedFrom":makeQuery(id+"F12.opPattern","COPY",BODY,{"derivedFrom":makeQuery(id+"F10.opPattern","COPY",BODY,{"derivedFrom":makeQuery(id+"F7.opPattern","COPY",BODY,{"derivedFrom":makeQuery(id+"F6.opPattern","COPY",BODY,{"derivedFrom":makeQuery(id+"F3.opPattern","COPY",BODY,{"derivedFrom":makeQuery(id+"F2.opPattern","COPY",BODY,{"derivedFrom":makeQuery(id+"F1.opRevolve","SWEPT_BODY",BODY,{"disambiguationData":[OSD([sQuery(id+"F0.wireOp",EDGE,"E1")])]}),"instanceName":"1"}),"instanceName":"1"}),"instanceName":"1"}),"instanceName":"1"}),"instanceName":"1"}),"instanceName":"1"}),"instanceName":"1"});
            var Q2534;
            Q2534=makeQuery(id+"F13.opPattern","COPY",BODY,{"derivedFrom":makeQuery(id+"F12.opPattern","COPY",BODY,{"derivedFrom":makeQuery(id+"F10.opPattern","COPY",BODY,{"derivedFrom":makeQuery(id+"F7.opPattern","COPY",BODY,{"derivedFrom":makeQuery(id+"F6.opPattern","COPY",BODY,{"derivedFrom":makeQuery(id+"F4.opPattern","COPY",BODY,{"derivedFrom":makeQuery(id+"F1.opRevolve","SWEPT_BODY",BODY,{"disambiguationData":[OSD([sQuery(id+"F0.wireOp",EDGE,"E1")])]}),"instanceName":"1"}),"instanceName":"1"}),"instanceName":"1"}),"instanceName":"1"}),"instanceName":"1"}),"instanceName":"1"});
            var Q2535;
            Q2535=makeQuery(id+"F13.opPattern","COPY",BODY,{"derivedFrom":makeQuery(id+"F12.opPattern","COPY",BODY,{"derivedFrom":makeQuery(id+"F10.opPattern","COPY",BODY,{"derivedFrom":makeQuery(id+"F7.opPattern","COPY",BODY,{"derivedFrom":makeQuery(id+"F6.opPattern","COPY",BODY,{"derivedFrom":makeQuery(id+"F4.opPattern","COPY",BODY,{"derivedFrom":makeQuery(id+"F2.opPattern","COPY",BODY,{"derivedFrom":makeQuery(id+"F1.opRevolve","SWEPT_BODY",BODY,{"disambiguationData":[OSD([sQuery(id+"F0.wireOp",EDGE,"E1")])]}),"instanceName":"1"}),"instanceName":"1"}),"instanceName":"1"}),"instanceName":"1"}),"instanceName":"1"}),"instanceName":"1"}),"instanceName":"1"});
            var Q2536;
            Q2536=makeQuery(id+"F13.opPattern","COPY",BODY,{"derivedFrom":makeQuery(id+"F12.opPattern","COPY",BODY,{"derivedFrom":makeQuery(id+"F10.opPattern","COPY",BODY,{"derivedFrom":makeQuery(id+"F7.opPattern","COPY",BODY,{"derivedFrom":makeQuery(id+"F6.opPattern","COPY",BODY,{"derivedFrom":makeQuery(id+"F4.opPattern","COPY",BODY,{"derivedFrom":makeQuery(id+"F3.opPattern","COPY",BODY,{"derivedFrom":makeQuery(id+"F2.opPattern","COPY",BODY,{"derivedFrom":makeQuery(id+"F1.opRevolve","SWEPT_BODY",BODY,{"disambiguationData":[OSD([sQuery(id+"F0.wireOp",EDGE,"E1")])]}),"instanceName":"1"}),"instanceName":"1"}),"instanceName":"1"}),"instanceName":"1"}),"instanceName":"1"}),"instanceName":"1"}),"instanceName":"1"}),"instanceName":"1"});
            var Q2537;
            Q2537=makeQuery(id+"F13.opPattern","COPY",BODY,{"derivedFrom":makeQuery(id+"F12.opPattern","COPY",BODY,{"derivedFrom":makeQuery(id+"F10.opPattern","COPY",BODY,{"derivedFrom":makeQuery(id+"F7.opPattern","COPY",BODY,{"derivedFrom":makeQuery(id+"F6.opPattern","COPY",BODY,{"derivedFrom":makeQuery(id+"F5.opPattern","COPY",BODY,{"derivedFrom":makeQuery(id+"F1.opRevolve","SWEPT_BODY",BODY,{"disambiguationData":[OSD([sQuery(id+"F0.wireOp",EDGE,"E1")])]}),"instanceName":"1"}),"instanceName":"1"}),"instanceName":"1"}),"instanceName":"1"}),"instanceName":"1"}),"instanceName":"1"});
            var Q2538;
            Q2538=makeQuery(id+"F13.opPattern","COPY",BODY,{"derivedFrom":makeQuery(id+"F12.opPattern","COPY",BODY,{"derivedFrom":makeQuery(id+"F10.opPattern","COPY",BODY,{"derivedFrom":makeQuery(id+"F7.opPattern","COPY",BODY,{"derivedFrom":makeQuery(id+"F6.opPattern","COPY",BODY,{"derivedFrom":makeQuery(id+"F5.opPattern","COPY",BODY,{"derivedFrom":makeQuery(id+"F2.opPattern","COPY",BODY,{"derivedFrom":makeQuery(id+"F1.opRevolve","SWEPT_BODY",BODY,{"disambiguationData":[OSD([sQuery(id+"F0.wireOp",EDGE,"E1")])]}),"instanceName":"1"}),"instanceName":"1"}),"instanceName":"1"}),"instanceName":"1"}),"instanceName":"1"}),"instanceName":"1"}),"instanceName":"1"});
            var Q2539;
            Q2539=makeQuery(id+"F13.opPattern","COPY",BODY,{"derivedFrom":makeQuery(id+"F12.opPattern","COPY",BODY,{"derivedFrom":makeQuery(id+"F10.opPattern","COPY",BODY,{"derivedFrom":makeQuery(id+"F7.opPattern","COPY",BODY,{"derivedFrom":makeQuery(id+"F6.opPattern","COPY",BODY,{"derivedFrom":makeQuery(id+"F5.opPattern","COPY",BODY,{"derivedFrom":makeQuery(id+"F3.opPattern","COPY",BODY,{"derivedFrom":makeQuery(id+"F2.opPattern","COPY",BODY,{"derivedFrom":makeQuery(id+"F1.opRevolve","SWEPT_BODY",BODY,{"disambiguationData":[OSD([sQuery(id+"F0.wireOp",EDGE,"E1")])]}),"instanceName":"1"}),"instanceName":"1"}),"instanceName":"1"}),"instanceName":"1"}),"instanceName":"1"}),"instanceName":"1"}),"instanceName":"1"}),"instanceName":"1"});
            var Q2540;
            Q2540=makeQuery(id+"F13.opPattern","COPY",BODY,{"derivedFrom":makeQuery(id+"F12.opPattern","COPY",BODY,{"derivedFrom":makeQuery(id+"F10.opPattern","COPY",BODY,{"derivedFrom":makeQuery(id+"F7.opPattern","COPY",BODY,{"derivedFrom":makeQuery(id+"F6.opPattern","COPY",BODY,{"derivedFrom":makeQuery(id+"F5.opPattern","COPY",BODY,{"derivedFrom":makeQuery(id+"F4.opPattern","COPY",BODY,{"derivedFrom":makeQuery(id+"F1.opRevolve","SWEPT_BODY",BODY,{"disambiguationData":[OSD([sQuery(id+"F0.wireOp",EDGE,"E1")])]}),"instanceName":"1"}),"instanceName":"1"}),"instanceName":"1"}),"instanceName":"1"}),"instanceName":"1"}),"instanceName":"1"}),"instanceName":"1"});
            var Q2541;
            Q2541=makeQuery(id+"F13.opPattern","COPY",BODY,{"derivedFrom":makeQuery(id+"F12.opPattern","COPY",BODY,{"derivedFrom":makeQuery(id+"F10.opPattern","COPY",BODY,{"derivedFrom":makeQuery(id+"F7.opPattern","COPY",BODY,{"derivedFrom":makeQuery(id+"F6.opPattern","COPY",BODY,{"derivedFrom":makeQuery(id+"F5.opPattern","COPY",BODY,{"derivedFrom":makeQuery(id+"F4.opPattern","COPY",BODY,{"derivedFrom":makeQuery(id+"F2.opPattern","COPY",BODY,{"derivedFrom":makeQuery(id+"F1.opRevolve","SWEPT_BODY",BODY,{"disambiguationData":[OSD([sQuery(id+"F0.wireOp",EDGE,"E1")])]}),"instanceName":"1"}),"instanceName":"1"}),"instanceName":"1"}),"instanceName":"1"}),"instanceName":"1"}),"instanceName":"1"}),"instanceName":"1"}),"instanceName":"1"});
            var Q2542;
            Q2542=makeQuery(id+"F13.opPattern","COPY",BODY,{"derivedFrom":makeQuery(id+"F12.opPattern","COPY",BODY,{"derivedFrom":makeQuery(id+"F10.opPattern","COPY",BODY,{"derivedFrom":makeQuery(id+"F7.opPattern","COPY",BODY,{"derivedFrom":makeQuery(id+"F6.opPattern","COPY",BODY,{"derivedFrom":makeQuery(id+"F5.opPattern","COPY",BODY,{"derivedFrom":makeQuery(id+"F4.opPattern","COPY",BODY,{"derivedFrom":makeQuery(id+"F3.opPattern","COPY",BODY,{"derivedFrom":makeQuery(id+"F2.opPattern","COPY",BODY,{"derivedFrom":makeQuery(id+"F1.opRevolve","SWEPT_BODY",BODY,{"disambiguationData":[OSD([sQuery(id+"F0.wireOp",EDGE,"E1")])]}),"instanceName":"1"}),"instanceName":"1"}),"instanceName":"1"}),"instanceName":"1"}),"instanceName":"1"}),"instanceName":"1"}),"instanceName":"1"}),"instanceName":"1"}),"instanceName":"1"});
            var Q2543;
            Q2543=makeQuery(id+"F13.opPattern","COPY",BODY,{"derivedFrom":makeQuery(id+"F12.opPattern","COPY",BODY,{"derivedFrom":makeQuery(id+"F10.opPattern","COPY",BODY,{"derivedFrom":makeQuery(id+"F8.opPattern","COPY",BODY,{"derivedFrom":makeQuery(id+"F1.opRevolve","SWEPT_BODY",BODY,{"disambiguationData":[OSD([sQuery(id+"F0.wireOp",EDGE,"E1")])]}),"instanceName":"1"}),"instanceName":"1"}),"instanceName":"1"}),"instanceName":"1"});
            var Q2544;
            Q2544=makeQuery(id+"F13.opPattern","COPY",BODY,{"derivedFrom":makeQuery(id+"F12.opPattern","COPY",BODY,{"derivedFrom":makeQuery(id+"F10.opPattern","COPY",BODY,{"derivedFrom":makeQuery(id+"F8.opPattern","COPY",BODY,{"derivedFrom":makeQuery(id+"F2.opPattern","COPY",BODY,{"derivedFrom":makeQuery(id+"F1.opRevolve","SWEPT_BODY",BODY,{"disambiguationData":[OSD([sQuery(id+"F0.wireOp",EDGE,"E1")])]}),"instanceName":"1"}),"instanceName":"1"}),"instanceName":"1"}),"instanceName":"1"}),"instanceName":"1"});
            var Q2545;
            Q2545=makeQuery(id+"F13.opPattern","COPY",BODY,{"derivedFrom":makeQuery(id+"F12.opPattern","COPY",BODY,{"derivedFrom":makeQuery(id+"F10.opPattern","COPY",BODY,{"derivedFrom":makeQuery(id+"F8.opPattern","COPY",BODY,{"derivedFrom":makeQuery(id+"F3.opPattern","COPY",BODY,{"derivedFrom":makeQuery(id+"F2.opPattern","COPY",BODY,{"derivedFrom":makeQuery(id+"F1.opRevolve","SWEPT_BODY",BODY,{"disambiguationData":[OSD([sQuery(id+"F0.wireOp",EDGE,"E1")])]}),"instanceName":"1"}),"instanceName":"1"}),"instanceName":"1"}),"instanceName":"1"}),"instanceName":"1"}),"instanceName":"1"});
            var Q2546;
            Q2546=makeQuery(id+"F13.opPattern","COPY",BODY,{"derivedFrom":makeQuery(id+"F12.opPattern","COPY",BODY,{"derivedFrom":makeQuery(id+"F10.opPattern","COPY",BODY,{"derivedFrom":makeQuery(id+"F8.opPattern","COPY",BODY,{"derivedFrom":makeQuery(id+"F4.opPattern","COPY",BODY,{"derivedFrom":makeQuery(id+"F1.opRevolve","SWEPT_BODY",BODY,{"disambiguationData":[OSD([sQuery(id+"F0.wireOp",EDGE,"E1")])]}),"instanceName":"1"}),"instanceName":"1"}),"instanceName":"1"}),"instanceName":"1"}),"instanceName":"1"});
            var Q2547;
            Q2547=makeQuery(id+"F13.opPattern","COPY",BODY,{"derivedFrom":makeQuery(id+"F12.opPattern","COPY",BODY,{"derivedFrom":makeQuery(id+"F10.opPattern","COPY",BODY,{"derivedFrom":makeQuery(id+"F8.opPattern","COPY",BODY,{"derivedFrom":makeQuery(id+"F4.opPattern","COPY",BODY,{"derivedFrom":makeQuery(id+"F2.opPattern","COPY",BODY,{"derivedFrom":makeQuery(id+"F1.opRevolve","SWEPT_BODY",BODY,{"disambiguationData":[OSD([sQuery(id+"F0.wireOp",EDGE,"E1")])]}),"instanceName":"1"}),"instanceName":"1"}),"instanceName":"1"}),"instanceName":"1"}),"instanceName":"1"}),"instanceName":"1"});
            var Q2548;
            Q2548=makeQuery(id+"F13.opPattern","COPY",BODY,{"derivedFrom":makeQuery(id+"F12.opPattern","COPY",BODY,{"derivedFrom":makeQuery(id+"F10.opPattern","COPY",BODY,{"derivedFrom":makeQuery(id+"F8.opPattern","COPY",BODY,{"derivedFrom":makeQuery(id+"F4.opPattern","COPY",BODY,{"derivedFrom":makeQuery(id+"F3.opPattern","COPY",BODY,{"derivedFrom":makeQuery(id+"F2.opPattern","COPY",BODY,{"derivedFrom":makeQuery(id+"F1.opRevolve","SWEPT_BODY",BODY,{"disambiguationData":[OSD([sQuery(id+"F0.wireOp",EDGE,"E1")])]}),"instanceName":"1"}),"instanceName":"1"}),"instanceName":"1"}),"instanceName":"1"}),"instanceName":"1"}),"instanceName":"1"}),"instanceName":"1"});
            var Q2549;
            Q2549=makeQuery(id+"F13.opPattern","COPY",BODY,{"derivedFrom":makeQuery(id+"F12.opPattern","COPY",BODY,{"derivedFrom":makeQuery(id+"F10.opPattern","COPY",BODY,{"derivedFrom":makeQuery(id+"F8.opPattern","COPY",BODY,{"derivedFrom":makeQuery(id+"F5.opPattern","COPY",BODY,{"derivedFrom":makeQuery(id+"F1.opRevolve","SWEPT_BODY",BODY,{"disambiguationData":[OSD([sQuery(id+"F0.wireOp",EDGE,"E1")])]}),"instanceName":"1"}),"instanceName":"1"}),"instanceName":"1"}),"instanceName":"1"}),"instanceName":"1"});
            var Q2550;
            Q2550=makeQuery(id+"F13.opPattern","COPY",BODY,{"derivedFrom":makeQuery(id+"F12.opPattern","COPY",BODY,{"derivedFrom":makeQuery(id+"F10.opPattern","COPY",BODY,{"derivedFrom":makeQuery(id+"F8.opPattern","COPY",BODY,{"derivedFrom":makeQuery(id+"F5.opPattern","COPY",BODY,{"derivedFrom":makeQuery(id+"F2.opPattern","COPY",BODY,{"derivedFrom":makeQuery(id+"F1.opRevolve","SWEPT_BODY",BODY,{"disambiguationData":[OSD([sQuery(id+"F0.wireOp",EDGE,"E1")])]}),"instanceName":"1"}),"instanceName":"1"}),"instanceName":"1"}),"instanceName":"1"}),"instanceName":"1"}),"instanceName":"1"});
            var Q2551;
            Q2551=makeQuery(id+"F13.opPattern","COPY",BODY,{"derivedFrom":makeQuery(id+"F12.opPattern","COPY",BODY,{"derivedFrom":makeQuery(id+"F10.opPattern","COPY",BODY,{"derivedFrom":makeQuery(id+"F8.opPattern","COPY",BODY,{"derivedFrom":makeQuery(id+"F5.opPattern","COPY",BODY,{"derivedFrom":makeQuery(id+"F3.opPattern","COPY",BODY,{"derivedFrom":makeQuery(id+"F2.opPattern","COPY",BODY,{"derivedFrom":makeQuery(id+"F1.opRevolve","SWEPT_BODY",BODY,{"disambiguationData":[OSD([sQuery(id+"F0.wireOp",EDGE,"E1")])]}),"instanceName":"1"}),"instanceName":"1"}),"instanceName":"1"}),"instanceName":"1"}),"instanceName":"1"}),"instanceName":"1"}),"instanceName":"1"});
            var Q2552;
            Q2552=makeQuery(id+"F13.opPattern","COPY",BODY,{"derivedFrom":makeQuery(id+"F12.opPattern","COPY",BODY,{"derivedFrom":makeQuery(id+"F10.opPattern","COPY",BODY,{"derivedFrom":makeQuery(id+"F8.opPattern","COPY",BODY,{"derivedFrom":makeQuery(id+"F5.opPattern","COPY",BODY,{"derivedFrom":makeQuery(id+"F4.opPattern","COPY",BODY,{"derivedFrom":makeQuery(id+"F1.opRevolve","SWEPT_BODY",BODY,{"disambiguationData":[OSD([sQuery(id+"F0.wireOp",EDGE,"E1")])]}),"instanceName":"1"}),"instanceName":"1"}),"instanceName":"1"}),"instanceName":"1"}),"instanceName":"1"}),"instanceName":"1"});
            var Q2553;
            Q2553=makeQuery(id+"F13.opPattern","COPY",BODY,{"derivedFrom":makeQuery(id+"F12.opPattern","COPY",BODY,{"derivedFrom":makeQuery(id+"F10.opPattern","COPY",BODY,{"derivedFrom":makeQuery(id+"F8.opPattern","COPY",BODY,{"derivedFrom":makeQuery(id+"F5.opPattern","COPY",BODY,{"derivedFrom":makeQuery(id+"F4.opPattern","COPY",BODY,{"derivedFrom":makeQuery(id+"F2.opPattern","COPY",BODY,{"derivedFrom":makeQuery(id+"F1.opRevolve","SWEPT_BODY",BODY,{"disambiguationData":[OSD([sQuery(id+"F0.wireOp",EDGE,"E1")])]}),"instanceName":"1"}),"instanceName":"1"}),"instanceName":"1"}),"instanceName":"1"}),"instanceName":"1"}),"instanceName":"1"}),"instanceName":"1"});
            var Q2554;
            Q2554=makeQuery(id+"F13.opPattern","COPY",BODY,{"derivedFrom":makeQuery(id+"F12.opPattern","COPY",BODY,{"derivedFrom":makeQuery(id+"F10.opPattern","COPY",BODY,{"derivedFrom":makeQuery(id+"F8.opPattern","COPY",BODY,{"derivedFrom":makeQuery(id+"F5.opPattern","COPY",BODY,{"derivedFrom":makeQuery(id+"F4.opPattern","COPY",BODY,{"derivedFrom":makeQuery(id+"F3.opPattern","COPY",BODY,{"derivedFrom":makeQuery(id+"F2.opPattern","COPY",BODY,{"derivedFrom":makeQuery(id+"F1.opRevolve","SWEPT_BODY",BODY,{"disambiguationData":[OSD([sQuery(id+"F0.wireOp",EDGE,"E1")])]}),"instanceName":"1"}),"instanceName":"1"}),"instanceName":"1"}),"instanceName":"1"}),"instanceName":"1"}),"instanceName":"1"}),"instanceName":"1"}),"instanceName":"1"});
            var Q2555;
            Q2555=makeQuery(id+"F13.opPattern","COPY",BODY,{"derivedFrom":makeQuery(id+"F12.opPattern","COPY",BODY,{"derivedFrom":makeQuery(id+"F10.opPattern","COPY",BODY,{"derivedFrom":makeQuery(id+"F8.opPattern","COPY",BODY,{"derivedFrom":makeQuery(id+"F6.opPattern","COPY",BODY,{"derivedFrom":makeQuery(id+"F1.opRevolve","SWEPT_BODY",BODY,{"disambiguationData":[OSD([sQuery(id+"F0.wireOp",EDGE,"E1")])]}),"instanceName":"1"}),"instanceName":"1"}),"instanceName":"1"}),"instanceName":"1"}),"instanceName":"1"});
            var Q2556;
            Q2556=makeQuery(id+"F13.opPattern","COPY",BODY,{"derivedFrom":makeQuery(id+"F12.opPattern","COPY",BODY,{"derivedFrom":makeQuery(id+"F10.opPattern","COPY",BODY,{"derivedFrom":makeQuery(id+"F8.opPattern","COPY",BODY,{"derivedFrom":makeQuery(id+"F6.opPattern","COPY",BODY,{"derivedFrom":makeQuery(id+"F2.opPattern","COPY",BODY,{"derivedFrom":makeQuery(id+"F1.opRevolve","SWEPT_BODY",BODY,{"disambiguationData":[OSD([sQuery(id+"F0.wireOp",EDGE,"E1")])]}),"instanceName":"1"}),"instanceName":"1"}),"instanceName":"1"}),"instanceName":"1"}),"instanceName":"1"}),"instanceName":"1"});
            var Q2557;
            Q2557=makeQuery(id+"F13.opPattern","COPY",BODY,{"derivedFrom":makeQuery(id+"F12.opPattern","COPY",BODY,{"derivedFrom":makeQuery(id+"F10.opPattern","COPY",BODY,{"derivedFrom":makeQuery(id+"F8.opPattern","COPY",BODY,{"derivedFrom":makeQuery(id+"F6.opPattern","COPY",BODY,{"derivedFrom":makeQuery(id+"F3.opPattern","COPY",BODY,{"derivedFrom":makeQuery(id+"F2.opPattern","COPY",BODY,{"derivedFrom":makeQuery(id+"F1.opRevolve","SWEPT_BODY",BODY,{"disambiguationData":[OSD([sQuery(id+"F0.wireOp",EDGE,"E1")])]}),"instanceName":"1"}),"instanceName":"1"}),"instanceName":"1"}),"instanceName":"1"}),"instanceName":"1"}),"instanceName":"1"}),"instanceName":"1"});
            var Q2558;
            Q2558=makeQuery(id+"F13.opPattern","COPY",BODY,{"derivedFrom":makeQuery(id+"F12.opPattern","COPY",BODY,{"derivedFrom":makeQuery(id+"F10.opPattern","COPY",BODY,{"derivedFrom":makeQuery(id+"F8.opPattern","COPY",BODY,{"derivedFrom":makeQuery(id+"F6.opPattern","COPY",BODY,{"derivedFrom":makeQuery(id+"F4.opPattern","COPY",BODY,{"derivedFrom":makeQuery(id+"F1.opRevolve","SWEPT_BODY",BODY,{"disambiguationData":[OSD([sQuery(id+"F0.wireOp",EDGE,"E1")])]}),"instanceName":"1"}),"instanceName":"1"}),"instanceName":"1"}),"instanceName":"1"}),"instanceName":"1"}),"instanceName":"1"});
            var Q2559;
            Q2559=makeQuery(id+"F13.opPattern","COPY",BODY,{"derivedFrom":makeQuery(id+"F12.opPattern","COPY",BODY,{"derivedFrom":makeQuery(id+"F10.opPattern","COPY",BODY,{"derivedFrom":makeQuery(id+"F8.opPattern","COPY",BODY,{"derivedFrom":makeQuery(id+"F6.opPattern","COPY",BODY,{"derivedFrom":makeQuery(id+"F4.opPattern","COPY",BODY,{"derivedFrom":makeQuery(id+"F2.opPattern","COPY",BODY,{"derivedFrom":makeQuery(id+"F1.opRevolve","SWEPT_BODY",BODY,{"disambiguationData":[OSD([sQuery(id+"F0.wireOp",EDGE,"E1")])]}),"instanceName":"1"}),"instanceName":"1"}),"instanceName":"1"}),"instanceName":"1"}),"instanceName":"1"}),"instanceName":"1"}),"instanceName":"1"});
            var Q2560;
            Q2560=makeQuery(id+"F13.opPattern","COPY",BODY,{"derivedFrom":makeQuery(id+"F12.opPattern","COPY",BODY,{"derivedFrom":makeQuery(id+"F10.opPattern","COPY",BODY,{"derivedFrom":makeQuery(id+"F8.opPattern","COPY",BODY,{"derivedFrom":makeQuery(id+"F6.opPattern","COPY",BODY,{"derivedFrom":makeQuery(id+"F4.opPattern","COPY",BODY,{"derivedFrom":makeQuery(id+"F3.opPattern","COPY",BODY,{"derivedFrom":makeQuery(id+"F2.opPattern","COPY",BODY,{"derivedFrom":makeQuery(id+"F1.opRevolve","SWEPT_BODY",BODY,{"disambiguationData":[OSD([sQuery(id+"F0.wireOp",EDGE,"E1")])]}),"instanceName":"1"}),"instanceName":"1"}),"instanceName":"1"}),"instanceName":"1"}),"instanceName":"1"}),"instanceName":"1"}),"instanceName":"1"}),"instanceName":"1"});
            var Q2561;
            Q2561=makeQuery(id+"F13.opPattern","COPY",BODY,{"derivedFrom":makeQuery(id+"F12.opPattern","COPY",BODY,{"derivedFrom":makeQuery(id+"F10.opPattern","COPY",BODY,{"derivedFrom":makeQuery(id+"F8.opPattern","COPY",BODY,{"derivedFrom":makeQuery(id+"F6.opPattern","COPY",BODY,{"derivedFrom":makeQuery(id+"F5.opPattern","COPY",BODY,{"derivedFrom":makeQuery(id+"F1.opRevolve","SWEPT_BODY",BODY,{"disambiguationData":[OSD([sQuery(id+"F0.wireOp",EDGE,"E1")])]}),"instanceName":"1"}),"instanceName":"1"}),"instanceName":"1"}),"instanceName":"1"}),"instanceName":"1"}),"instanceName":"1"});
            var Q2562;
            Q2562=makeQuery(id+"F13.opPattern","COPY",BODY,{"derivedFrom":makeQuery(id+"F12.opPattern","COPY",BODY,{"derivedFrom":makeQuery(id+"F10.opPattern","COPY",BODY,{"derivedFrom":makeQuery(id+"F8.opPattern","COPY",BODY,{"derivedFrom":makeQuery(id+"F6.opPattern","COPY",BODY,{"derivedFrom":makeQuery(id+"F5.opPattern","COPY",BODY,{"derivedFrom":makeQuery(id+"F2.opPattern","COPY",BODY,{"derivedFrom":makeQuery(id+"F1.opRevolve","SWEPT_BODY",BODY,{"disambiguationData":[OSD([sQuery(id+"F0.wireOp",EDGE,"E1")])]}),"instanceName":"1"}),"instanceName":"1"}),"instanceName":"1"}),"instanceName":"1"}),"instanceName":"1"}),"instanceName":"1"}),"instanceName":"1"});
            var Q2563;
            Q2563=makeQuery(id+"F13.opPattern","COPY",BODY,{"derivedFrom":makeQuery(id+"F12.opPattern","COPY",BODY,{"derivedFrom":makeQuery(id+"F10.opPattern","COPY",BODY,{"derivedFrom":makeQuery(id+"F8.opPattern","COPY",BODY,{"derivedFrom":makeQuery(id+"F6.opPattern","COPY",BODY,{"derivedFrom":makeQuery(id+"F5.opPattern","COPY",BODY,{"derivedFrom":makeQuery(id+"F3.opPattern","COPY",BODY,{"derivedFrom":makeQuery(id+"F2.opPattern","COPY",BODY,{"derivedFrom":makeQuery(id+"F1.opRevolve","SWEPT_BODY",BODY,{"disambiguationData":[OSD([sQuery(id+"F0.wireOp",EDGE,"E1")])]}),"instanceName":"1"}),"instanceName":"1"}),"instanceName":"1"}),"instanceName":"1"}),"instanceName":"1"}),"instanceName":"1"}),"instanceName":"1"}),"instanceName":"1"});
            var Q2564;
            Q2564=makeQuery(id+"F13.opPattern","COPY",BODY,{"derivedFrom":makeQuery(id+"F12.opPattern","COPY",BODY,{"derivedFrom":makeQuery(id+"F10.opPattern","COPY",BODY,{"derivedFrom":makeQuery(id+"F8.opPattern","COPY",BODY,{"derivedFrom":makeQuery(id+"F6.opPattern","COPY",BODY,{"derivedFrom":makeQuery(id+"F5.opPattern","COPY",BODY,{"derivedFrom":makeQuery(id+"F4.opPattern","COPY",BODY,{"derivedFrom":makeQuery(id+"F1.opRevolve","SWEPT_BODY",BODY,{"disambiguationData":[OSD([sQuery(id+"F0.wireOp",EDGE,"E1")])]}),"instanceName":"1"}),"instanceName":"1"}),"instanceName":"1"}),"instanceName":"1"}),"instanceName":"1"}),"instanceName":"1"}),"instanceName":"1"});
            var Q2565;
            Q2565=makeQuery(id+"F13.opPattern","COPY",BODY,{"derivedFrom":makeQuery(id+"F12.opPattern","COPY",BODY,{"derivedFrom":makeQuery(id+"F10.opPattern","COPY",BODY,{"derivedFrom":makeQuery(id+"F8.opPattern","COPY",BODY,{"derivedFrom":makeQuery(id+"F6.opPattern","COPY",BODY,{"derivedFrom":makeQuery(id+"F5.opPattern","COPY",BODY,{"derivedFrom":makeQuery(id+"F4.opPattern","COPY",BODY,{"derivedFrom":makeQuery(id+"F2.opPattern","COPY",BODY,{"derivedFrom":makeQuery(id+"F1.opRevolve","SWEPT_BODY",BODY,{"disambiguationData":[OSD([sQuery(id+"F0.wireOp",EDGE,"E1")])]}),"instanceName":"1"}),"instanceName":"1"}),"instanceName":"1"}),"instanceName":"1"}),"instanceName":"1"}),"instanceName":"1"}),"instanceName":"1"}),"instanceName":"1"});
            var Q2566;
            Q2566=makeQuery(id+"F13.opPattern","COPY",BODY,{"derivedFrom":makeQuery(id+"F12.opPattern","COPY",BODY,{"derivedFrom":makeQuery(id+"F10.opPattern","COPY",BODY,{"derivedFrom":makeQuery(id+"F8.opPattern","COPY",BODY,{"derivedFrom":makeQuery(id+"F6.opPattern","COPY",BODY,{"derivedFrom":makeQuery(id+"F5.opPattern","COPY",BODY,{"derivedFrom":makeQuery(id+"F4.opPattern","COPY",BODY,{"derivedFrom":makeQuery(id+"F3.opPattern","COPY",BODY,{"derivedFrom":makeQuery(id+"F2.opPattern","COPY",BODY,{"derivedFrom":makeQuery(id+"F1.opRevolve","SWEPT_BODY",BODY,{"disambiguationData":[OSD([sQuery(id+"F0.wireOp",EDGE,"E1")])]}),"instanceName":"1"}),"instanceName":"1"}),"instanceName":"1"}),"instanceName":"1"}),"instanceName":"1"}),"instanceName":"1"}),"instanceName":"1"}),"instanceName":"1"}),"instanceName":"1"});
            var Q2567;
            Q2567=makeQuery(id+"F13.opPattern","COPY",BODY,{"derivedFrom":makeQuery(id+"F12.opPattern","COPY",BODY,{"derivedFrom":makeQuery(id+"F10.opPattern","COPY",BODY,{"derivedFrom":makeQuery(id+"F8.opPattern","COPY",BODY,{"derivedFrom":makeQuery(id+"F7.opPattern","COPY",BODY,{"derivedFrom":makeQuery(id+"F1.opRevolve","SWEPT_BODY",BODY,{"disambiguationData":[OSD([sQuery(id+"F0.wireOp",EDGE,"E1")])]}),"instanceName":"1"}),"instanceName":"1"}),"instanceName":"1"}),"instanceName":"1"}),"instanceName":"1"});
            var Q2568;
            Q2568=makeQuery(id+"F13.opPattern","COPY",BODY,{"derivedFrom":makeQuery(id+"F12.opPattern","COPY",BODY,{"derivedFrom":makeQuery(id+"F10.opPattern","COPY",BODY,{"derivedFrom":makeQuery(id+"F8.opPattern","COPY",BODY,{"derivedFrom":makeQuery(id+"F7.opPattern","COPY",BODY,{"derivedFrom":makeQuery(id+"F2.opPattern","COPY",BODY,{"derivedFrom":makeQuery(id+"F1.opRevolve","SWEPT_BODY",BODY,{"disambiguationData":[OSD([sQuery(id+"F0.wireOp",EDGE,"E1")])]}),"instanceName":"1"}),"instanceName":"1"}),"instanceName":"1"}),"instanceName":"1"}),"instanceName":"1"}),"instanceName":"1"});
            var Q2569;
            Q2569=makeQuery(id+"F13.opPattern","COPY",BODY,{"derivedFrom":makeQuery(id+"F12.opPattern","COPY",BODY,{"derivedFrom":makeQuery(id+"F10.opPattern","COPY",BODY,{"derivedFrom":makeQuery(id+"F8.opPattern","COPY",BODY,{"derivedFrom":makeQuery(id+"F7.opPattern","COPY",BODY,{"derivedFrom":makeQuery(id+"F3.opPattern","COPY",BODY,{"derivedFrom":makeQuery(id+"F2.opPattern","COPY",BODY,{"derivedFrom":makeQuery(id+"F1.opRevolve","SWEPT_BODY",BODY,{"disambiguationData":[OSD([sQuery(id+"F0.wireOp",EDGE,"E1")])]}),"instanceName":"1"}),"instanceName":"1"}),"instanceName":"1"}),"instanceName":"1"}),"instanceName":"1"}),"instanceName":"1"}),"instanceName":"1"});
            var Q2570;
            Q2570=makeQuery(id+"F13.opPattern","COPY",BODY,{"derivedFrom":makeQuery(id+"F12.opPattern","COPY",BODY,{"derivedFrom":makeQuery(id+"F10.opPattern","COPY",BODY,{"derivedFrom":makeQuery(id+"F8.opPattern","COPY",BODY,{"derivedFrom":makeQuery(id+"F7.opPattern","COPY",BODY,{"derivedFrom":makeQuery(id+"F4.opPattern","COPY",BODY,{"derivedFrom":makeQuery(id+"F1.opRevolve","SWEPT_BODY",BODY,{"disambiguationData":[OSD([sQuery(id+"F0.wireOp",EDGE,"E1")])]}),"instanceName":"1"}),"instanceName":"1"}),"instanceName":"1"}),"instanceName":"1"}),"instanceName":"1"}),"instanceName":"1"});
            var Q2571;
            Q2571=makeQuery(id+"F13.opPattern","COPY",BODY,{"derivedFrom":makeQuery(id+"F12.opPattern","COPY",BODY,{"derivedFrom":makeQuery(id+"F10.opPattern","COPY",BODY,{"derivedFrom":makeQuery(id+"F8.opPattern","COPY",BODY,{"derivedFrom":makeQuery(id+"F7.opPattern","COPY",BODY,{"derivedFrom":makeQuery(id+"F4.opPattern","COPY",BODY,{"derivedFrom":makeQuery(id+"F2.opPattern","COPY",BODY,{"derivedFrom":makeQuery(id+"F1.opRevolve","SWEPT_BODY",BODY,{"disambiguationData":[OSD([sQuery(id+"F0.wireOp",EDGE,"E1")])]}),"instanceName":"1"}),"instanceName":"1"}),"instanceName":"1"}),"instanceName":"1"}),"instanceName":"1"}),"instanceName":"1"}),"instanceName":"1"});
            var Q2572;
            Q2572=makeQuery(id+"F13.opPattern","COPY",BODY,{"derivedFrom":makeQuery(id+"F12.opPattern","COPY",BODY,{"derivedFrom":makeQuery(id+"F10.opPattern","COPY",BODY,{"derivedFrom":makeQuery(id+"F8.opPattern","COPY",BODY,{"derivedFrom":makeQuery(id+"F7.opPattern","COPY",BODY,{"derivedFrom":makeQuery(id+"F4.opPattern","COPY",BODY,{"derivedFrom":makeQuery(id+"F3.opPattern","COPY",BODY,{"derivedFrom":makeQuery(id+"F2.opPattern","COPY",BODY,{"derivedFrom":makeQuery(id+"F1.opRevolve","SWEPT_BODY",BODY,{"disambiguationData":[OSD([sQuery(id+"F0.wireOp",EDGE,"E1")])]}),"instanceName":"1"}),"instanceName":"1"}),"instanceName":"1"}),"instanceName":"1"}),"instanceName":"1"}),"instanceName":"1"}),"instanceName":"1"}),"instanceName":"1"});
            var Q2573;
            Q2573=makeQuery(id+"F13.opPattern","COPY",BODY,{"derivedFrom":makeQuery(id+"F12.opPattern","COPY",BODY,{"derivedFrom":makeQuery(id+"F10.opPattern","COPY",BODY,{"derivedFrom":makeQuery(id+"F8.opPattern","COPY",BODY,{"derivedFrom":makeQuery(id+"F7.opPattern","COPY",BODY,{"derivedFrom":makeQuery(id+"F5.opPattern","COPY",BODY,{"derivedFrom":makeQuery(id+"F1.opRevolve","SWEPT_BODY",BODY,{"disambiguationData":[OSD([sQuery(id+"F0.wireOp",EDGE,"E1")])]}),"instanceName":"1"}),"instanceName":"1"}),"instanceName":"1"}),"instanceName":"1"}),"instanceName":"1"}),"instanceName":"1"});
            var Q2574;
            Q2574=makeQuery(id+"F13.opPattern","COPY",BODY,{"derivedFrom":makeQuery(id+"F12.opPattern","COPY",BODY,{"derivedFrom":makeQuery(id+"F10.opPattern","COPY",BODY,{"derivedFrom":makeQuery(id+"F8.opPattern","COPY",BODY,{"derivedFrom":makeQuery(id+"F7.opPattern","COPY",BODY,{"derivedFrom":makeQuery(id+"F5.opPattern","COPY",BODY,{"derivedFrom":makeQuery(id+"F2.opPattern","COPY",BODY,{"derivedFrom":makeQuery(id+"F1.opRevolve","SWEPT_BODY",BODY,{"disambiguationData":[OSD([sQuery(id+"F0.wireOp",EDGE,"E1")])]}),"instanceName":"1"}),"instanceName":"1"}),"instanceName":"1"}),"instanceName":"1"}),"instanceName":"1"}),"instanceName":"1"}),"instanceName":"1"});
            var Q2575;
            Q2575=makeQuery(id+"F13.opPattern","COPY",BODY,{"derivedFrom":makeQuery(id+"F12.opPattern","COPY",BODY,{"derivedFrom":makeQuery(id+"F10.opPattern","COPY",BODY,{"derivedFrom":makeQuery(id+"F8.opPattern","COPY",BODY,{"derivedFrom":makeQuery(id+"F7.opPattern","COPY",BODY,{"derivedFrom":makeQuery(id+"F5.opPattern","COPY",BODY,{"derivedFrom":makeQuery(id+"F3.opPattern","COPY",BODY,{"derivedFrom":makeQuery(id+"F2.opPattern","COPY",BODY,{"derivedFrom":makeQuery(id+"F1.opRevolve","SWEPT_BODY",BODY,{"disambiguationData":[OSD([sQuery(id+"F0.wireOp",EDGE,"E1")])]}),"instanceName":"1"}),"instanceName":"1"}),"instanceName":"1"}),"instanceName":"1"}),"instanceName":"1"}),"instanceName":"1"}),"instanceName":"1"}),"instanceName":"1"});
            var Q2576;
            Q2576=makeQuery(id+"F13.opPattern","COPY",BODY,{"derivedFrom":makeQuery(id+"F12.opPattern","COPY",BODY,{"derivedFrom":makeQuery(id+"F10.opPattern","COPY",BODY,{"derivedFrom":makeQuery(id+"F8.opPattern","COPY",BODY,{"derivedFrom":makeQuery(id+"F7.opPattern","COPY",BODY,{"derivedFrom":makeQuery(id+"F5.opPattern","COPY",BODY,{"derivedFrom":makeQuery(id+"F4.opPattern","COPY",BODY,{"derivedFrom":makeQuery(id+"F1.opRevolve","SWEPT_BODY",BODY,{"disambiguationData":[OSD([sQuery(id+"F0.wireOp",EDGE,"E1")])]}),"instanceName":"1"}),"instanceName":"1"}),"instanceName":"1"}),"instanceName":"1"}),"instanceName":"1"}),"instanceName":"1"}),"instanceName":"1"});
            var Q2577;
            Q2577=makeQuery(id+"F13.opPattern","COPY",BODY,{"derivedFrom":makeQuery(id+"F12.opPattern","COPY",BODY,{"derivedFrom":makeQuery(id+"F10.opPattern","COPY",BODY,{"derivedFrom":makeQuery(id+"F8.opPattern","COPY",BODY,{"derivedFrom":makeQuery(id+"F7.opPattern","COPY",BODY,{"derivedFrom":makeQuery(id+"F5.opPattern","COPY",BODY,{"derivedFrom":makeQuery(id+"F4.opPattern","COPY",BODY,{"derivedFrom":makeQuery(id+"F2.opPattern","COPY",BODY,{"derivedFrom":makeQuery(id+"F1.opRevolve","SWEPT_BODY",BODY,{"disambiguationData":[OSD([sQuery(id+"F0.wireOp",EDGE,"E1")])]}),"instanceName":"1"}),"instanceName":"1"}),"instanceName":"1"}),"instanceName":"1"}),"instanceName":"1"}),"instanceName":"1"}),"instanceName":"1"}),"instanceName":"1"});
            var Q2578;
            Q2578=makeQuery(id+"F13.opPattern","COPY",BODY,{"derivedFrom":makeQuery(id+"F12.opPattern","COPY",BODY,{"derivedFrom":makeQuery(id+"F10.opPattern","COPY",BODY,{"derivedFrom":makeQuery(id+"F8.opPattern","COPY",BODY,{"derivedFrom":makeQuery(id+"F7.opPattern","COPY",BODY,{"derivedFrom":makeQuery(id+"F5.opPattern","COPY",BODY,{"derivedFrom":makeQuery(id+"F4.opPattern","COPY",BODY,{"derivedFrom":makeQuery(id+"F3.opPattern","COPY",BODY,{"derivedFrom":makeQuery(id+"F2.opPattern","COPY",BODY,{"derivedFrom":makeQuery(id+"F1.opRevolve","SWEPT_BODY",BODY,{"disambiguationData":[OSD([sQuery(id+"F0.wireOp",EDGE,"E1")])]}),"instanceName":"1"}),"instanceName":"1"}),"instanceName":"1"}),"instanceName":"1"}),"instanceName":"1"}),"instanceName":"1"}),"instanceName":"1"}),"instanceName":"1"}),"instanceName":"1"});
            var Q2579;
            Q2579=makeQuery(id+"F13.opPattern","COPY",BODY,{"derivedFrom":makeQuery(id+"F12.opPattern","COPY",BODY,{"derivedFrom":makeQuery(id+"F10.opPattern","COPY",BODY,{"derivedFrom":makeQuery(id+"F8.opPattern","COPY",BODY,{"derivedFrom":makeQuery(id+"F7.opPattern","COPY",BODY,{"derivedFrom":makeQuery(id+"F6.opPattern","COPY",BODY,{"derivedFrom":makeQuery(id+"F1.opRevolve","SWEPT_BODY",BODY,{"disambiguationData":[OSD([sQuery(id+"F0.wireOp",EDGE,"E1")])]}),"instanceName":"1"}),"instanceName":"1"}),"instanceName":"1"}),"instanceName":"1"}),"instanceName":"1"}),"instanceName":"1"});
            var Q2580;
            Q2580=makeQuery(id+"F13.opPattern","COPY",BODY,{"derivedFrom":makeQuery(id+"F12.opPattern","COPY",BODY,{"derivedFrom":makeQuery(id+"F10.opPattern","COPY",BODY,{"derivedFrom":makeQuery(id+"F8.opPattern","COPY",BODY,{"derivedFrom":makeQuery(id+"F7.opPattern","COPY",BODY,{"derivedFrom":makeQuery(id+"F6.opPattern","COPY",BODY,{"derivedFrom":makeQuery(id+"F2.opPattern","COPY",BODY,{"derivedFrom":makeQuery(id+"F1.opRevolve","SWEPT_BODY",BODY,{"disambiguationData":[OSD([sQuery(id+"F0.wireOp",EDGE,"E1")])]}),"instanceName":"1"}),"instanceName":"1"}),"instanceName":"1"}),"instanceName":"1"}),"instanceName":"1"}),"instanceName":"1"}),"instanceName":"1"});
            var Q2581;
            Q2581=makeQuery(id+"F13.opPattern","COPY",BODY,{"derivedFrom":makeQuery(id+"F12.opPattern","COPY",BODY,{"derivedFrom":makeQuery(id+"F10.opPattern","COPY",BODY,{"derivedFrom":makeQuery(id+"F8.opPattern","COPY",BODY,{"derivedFrom":makeQuery(id+"F7.opPattern","COPY",BODY,{"derivedFrom":makeQuery(id+"F6.opPattern","COPY",BODY,{"derivedFrom":makeQuery(id+"F3.opPattern","COPY",BODY,{"derivedFrom":makeQuery(id+"F2.opPattern","COPY",BODY,{"derivedFrom":makeQuery(id+"F1.opRevolve","SWEPT_BODY",BODY,{"disambiguationData":[OSD([sQuery(id+"F0.wireOp",EDGE,"E1")])]}),"instanceName":"1"}),"instanceName":"1"}),"instanceName":"1"}),"instanceName":"1"}),"instanceName":"1"}),"instanceName":"1"}),"instanceName":"1"}),"instanceName":"1"});
            var Q2582;
            Q2582=makeQuery(id+"F13.opPattern","COPY",BODY,{"derivedFrom":makeQuery(id+"F12.opPattern","COPY",BODY,{"derivedFrom":makeQuery(id+"F10.opPattern","COPY",BODY,{"derivedFrom":makeQuery(id+"F8.opPattern","COPY",BODY,{"derivedFrom":makeQuery(id+"F7.opPattern","COPY",BODY,{"derivedFrom":makeQuery(id+"F6.opPattern","COPY",BODY,{"derivedFrom":makeQuery(id+"F4.opPattern","COPY",BODY,{"derivedFrom":makeQuery(id+"F1.opRevolve","SWEPT_BODY",BODY,{"disambiguationData":[OSD([sQuery(id+"F0.wireOp",EDGE,"E1")])]}),"instanceName":"1"}),"instanceName":"1"}),"instanceName":"1"}),"instanceName":"1"}),"instanceName":"1"}),"instanceName":"1"}),"instanceName":"1"});
            var Q2583;
            Q2583=makeQuery(id+"F13.opPattern","COPY",BODY,{"derivedFrom":makeQuery(id+"F12.opPattern","COPY",BODY,{"derivedFrom":makeQuery(id+"F10.opPattern","COPY",BODY,{"derivedFrom":makeQuery(id+"F8.opPattern","COPY",BODY,{"derivedFrom":makeQuery(id+"F7.opPattern","COPY",BODY,{"derivedFrom":makeQuery(id+"F6.opPattern","COPY",BODY,{"derivedFrom":makeQuery(id+"F4.opPattern","COPY",BODY,{"derivedFrom":makeQuery(id+"F2.opPattern","COPY",BODY,{"derivedFrom":makeQuery(id+"F1.opRevolve","SWEPT_BODY",BODY,{"disambiguationData":[OSD([sQuery(id+"F0.wireOp",EDGE,"E1")])]}),"instanceName":"1"}),"instanceName":"1"}),"instanceName":"1"}),"instanceName":"1"}),"instanceName":"1"}),"instanceName":"1"}),"instanceName":"1"}),"instanceName":"1"});
            var Q2584;
            Q2584=makeQuery(id+"F13.opPattern","COPY",BODY,{"derivedFrom":makeQuery(id+"F12.opPattern","COPY",BODY,{"derivedFrom":makeQuery(id+"F10.opPattern","COPY",BODY,{"derivedFrom":makeQuery(id+"F8.opPattern","COPY",BODY,{"derivedFrom":makeQuery(id+"F7.opPattern","COPY",BODY,{"derivedFrom":makeQuery(id+"F6.opPattern","COPY",BODY,{"derivedFrom":makeQuery(id+"F4.opPattern","COPY",BODY,{"derivedFrom":makeQuery(id+"F3.opPattern","COPY",BODY,{"derivedFrom":makeQuery(id+"F2.opPattern","COPY",BODY,{"derivedFrom":makeQuery(id+"F1.opRevolve","SWEPT_BODY",BODY,{"disambiguationData":[OSD([sQuery(id+"F0.wireOp",EDGE,"E1")])]}),"instanceName":"1"}),"instanceName":"1"}),"instanceName":"1"}),"instanceName":"1"}),"instanceName":"1"}),"instanceName":"1"}),"instanceName":"1"}),"instanceName":"1"}),"instanceName":"1"});
            var Q2585;
            Q2585=makeQuery(id+"F13.opPattern","COPY",BODY,{"derivedFrom":makeQuery(id+"F12.opPattern","COPY",BODY,{"derivedFrom":makeQuery(id+"F10.opPattern","COPY",BODY,{"derivedFrom":makeQuery(id+"F8.opPattern","COPY",BODY,{"derivedFrom":makeQuery(id+"F7.opPattern","COPY",BODY,{"derivedFrom":makeQuery(id+"F6.opPattern","COPY",BODY,{"derivedFrom":makeQuery(id+"F5.opPattern","COPY",BODY,{"derivedFrom":makeQuery(id+"F1.opRevolve","SWEPT_BODY",BODY,{"disambiguationData":[OSD([sQuery(id+"F0.wireOp",EDGE,"E1")])]}),"instanceName":"1"}),"instanceName":"1"}),"instanceName":"1"}),"instanceName":"1"}),"instanceName":"1"}),"instanceName":"1"}),"instanceName":"1"});
            var Q2586;
            Q2586=makeQuery(id+"F13.opPattern","COPY",BODY,{"derivedFrom":makeQuery(id+"F12.opPattern","COPY",BODY,{"derivedFrom":makeQuery(id+"F10.opPattern","COPY",BODY,{"derivedFrom":makeQuery(id+"F8.opPattern","COPY",BODY,{"derivedFrom":makeQuery(id+"F7.opPattern","COPY",BODY,{"derivedFrom":makeQuery(id+"F6.opPattern","COPY",BODY,{"derivedFrom":makeQuery(id+"F5.opPattern","COPY",BODY,{"derivedFrom":makeQuery(id+"F2.opPattern","COPY",BODY,{"derivedFrom":makeQuery(id+"F1.opRevolve","SWEPT_BODY",BODY,{"disambiguationData":[OSD([sQuery(id+"F0.wireOp",EDGE,"E1")])]}),"instanceName":"1"}),"instanceName":"1"}),"instanceName":"1"}),"instanceName":"1"}),"instanceName":"1"}),"instanceName":"1"}),"instanceName":"1"}),"instanceName":"1"});
            var Q2587;
            Q2587=makeQuery(id+"F13.opPattern","COPY",BODY,{"derivedFrom":makeQuery(id+"F12.opPattern","COPY",BODY,{"derivedFrom":makeQuery(id+"F10.opPattern","COPY",BODY,{"derivedFrom":makeQuery(id+"F8.opPattern","COPY",BODY,{"derivedFrom":makeQuery(id+"F7.opPattern","COPY",BODY,{"derivedFrom":makeQuery(id+"F6.opPattern","COPY",BODY,{"derivedFrom":makeQuery(id+"F5.opPattern","COPY",BODY,{"derivedFrom":makeQuery(id+"F3.opPattern","COPY",BODY,{"derivedFrom":makeQuery(id+"F2.opPattern","COPY",BODY,{"derivedFrom":makeQuery(id+"F1.opRevolve","SWEPT_BODY",BODY,{"disambiguationData":[OSD([sQuery(id+"F0.wireOp",EDGE,"E1")])]}),"instanceName":"1"}),"instanceName":"1"}),"instanceName":"1"}),"instanceName":"1"}),"instanceName":"1"}),"instanceName":"1"}),"instanceName":"1"}),"instanceName":"1"}),"instanceName":"1"});
            var Q2588;
            Q2588=makeQuery(id+"F13.opPattern","COPY",BODY,{"derivedFrom":makeQuery(id+"F12.opPattern","COPY",BODY,{"derivedFrom":makeQuery(id+"F10.opPattern","COPY",BODY,{"derivedFrom":makeQuery(id+"F8.opPattern","COPY",BODY,{"derivedFrom":makeQuery(id+"F7.opPattern","COPY",BODY,{"derivedFrom":makeQuery(id+"F6.opPattern","COPY",BODY,{"derivedFrom":makeQuery(id+"F5.opPattern","COPY",BODY,{"derivedFrom":makeQuery(id+"F4.opPattern","COPY",BODY,{"derivedFrom":makeQuery(id+"F1.opRevolve","SWEPT_BODY",BODY,{"disambiguationData":[OSD([sQuery(id+"F0.wireOp",EDGE,"E1")])]}),"instanceName":"1"}),"instanceName":"1"}),"instanceName":"1"}),"instanceName":"1"}),"instanceName":"1"}),"instanceName":"1"}),"instanceName":"1"}),"instanceName":"1"});
            var Q2589;
            Q2589=makeQuery(id+"F13.opPattern","COPY",BODY,{"derivedFrom":makeQuery(id+"F12.opPattern","COPY",BODY,{"derivedFrom":makeQuery(id+"F10.opPattern","COPY",BODY,{"derivedFrom":makeQuery(id+"F8.opPattern","COPY",BODY,{"derivedFrom":makeQuery(id+"F7.opPattern","COPY",BODY,{"derivedFrom":makeQuery(id+"F6.opPattern","COPY",BODY,{"derivedFrom":makeQuery(id+"F5.opPattern","COPY",BODY,{"derivedFrom":makeQuery(id+"F4.opPattern","COPY",BODY,{"derivedFrom":makeQuery(id+"F2.opPattern","COPY",BODY,{"derivedFrom":makeQuery(id+"F1.opRevolve","SWEPT_BODY",BODY,{"disambiguationData":[OSD([sQuery(id+"F0.wireOp",EDGE,"E1")])]}),"instanceName":"1"}),"instanceName":"1"}),"instanceName":"1"}),"instanceName":"1"}),"instanceName":"1"}),"instanceName":"1"}),"instanceName":"1"}),"instanceName":"1"}),"instanceName":"1"});
            var Q2590;
            Q2590=makeQuery(id+"F13.opPattern","COPY",BODY,{"derivedFrom":makeQuery(id+"F12.opPattern","COPY",BODY,{"derivedFrom":makeQuery(id+"F10.opPattern","COPY",BODY,{"derivedFrom":makeQuery(id+"F8.opPattern","COPY",BODY,{"derivedFrom":makeQuery(id+"F7.opPattern","COPY",BODY,{"derivedFrom":makeQuery(id+"F6.opPattern","COPY",BODY,{"derivedFrom":makeQuery(id+"F5.opPattern","COPY",BODY,{"derivedFrom":makeQuery(id+"F4.opPattern","COPY",BODY,{"derivedFrom":makeQuery(id+"F3.opPattern","COPY",BODY,{"derivedFrom":makeQuery(id+"F2.opPattern","COPY",BODY,{"derivedFrom":makeQuery(id+"F1.opRevolve","SWEPT_BODY",BODY,{"disambiguationData":[OSD([sQuery(id+"F0.wireOp",EDGE,"E1")])]}),"instanceName":"1"}),"instanceName":"1"}),"instanceName":"1"}),"instanceName":"1"}),"instanceName":"1"}),"instanceName":"1"}),"instanceName":"1"}),"instanceName":"1"}),"instanceName":"1"}),"instanceName":"1"});
            var Q2591;
            Q2591=makeQuery(id+"F13.opPattern","COPY",BODY,{"derivedFrom":makeQuery(id+"F12.opPattern","COPY",BODY,{"derivedFrom":makeQuery(id+"F10.opPattern","COPY",BODY,{"derivedFrom":makeQuery(id+"F9.opPattern","COPY",BODY,{"derivedFrom":makeQuery(id+"F1.opRevolve","SWEPT_BODY",BODY,{"disambiguationData":[OSD([sQuery(id+"F0.wireOp",EDGE,"E1")])]}),"instanceName":"1"}),"instanceName":"1"}),"instanceName":"1"}),"instanceName":"1"});
            var Q2592;
            Q2592=makeQuery(id+"F13.opPattern","COPY",BODY,{"derivedFrom":makeQuery(id+"F12.opPattern","COPY",BODY,{"derivedFrom":makeQuery(id+"F10.opPattern","COPY",BODY,{"derivedFrom":makeQuery(id+"F9.opPattern","COPY",BODY,{"derivedFrom":makeQuery(id+"F2.opPattern","COPY",BODY,{"derivedFrom":makeQuery(id+"F1.opRevolve","SWEPT_BODY",BODY,{"disambiguationData":[OSD([sQuery(id+"F0.wireOp",EDGE,"E1")])]}),"instanceName":"1"}),"instanceName":"1"}),"instanceName":"1"}),"instanceName":"1"}),"instanceName":"1"});
            var Q2593;
            Q2593=makeQuery(id+"F13.opPattern","COPY",BODY,{"derivedFrom":makeQuery(id+"F12.opPattern","COPY",BODY,{"derivedFrom":makeQuery(id+"F10.opPattern","COPY",BODY,{"derivedFrom":makeQuery(id+"F9.opPattern","COPY",BODY,{"derivedFrom":makeQuery(id+"F3.opPattern","COPY",BODY,{"derivedFrom":makeQuery(id+"F2.opPattern","COPY",BODY,{"derivedFrom":makeQuery(id+"F1.opRevolve","SWEPT_BODY",BODY,{"disambiguationData":[OSD([sQuery(id+"F0.wireOp",EDGE,"E1")])]}),"instanceName":"1"}),"instanceName":"1"}),"instanceName":"1"}),"instanceName":"1"}),"instanceName":"1"}),"instanceName":"1"});
            var Q2594;
            Q2594=makeQuery(id+"F13.opPattern","COPY",BODY,{"derivedFrom":makeQuery(id+"F12.opPattern","COPY",BODY,{"derivedFrom":makeQuery(id+"F10.opPattern","COPY",BODY,{"derivedFrom":makeQuery(id+"F9.opPattern","COPY",BODY,{"derivedFrom":makeQuery(id+"F4.opPattern","COPY",BODY,{"derivedFrom":makeQuery(id+"F1.opRevolve","SWEPT_BODY",BODY,{"disambiguationData":[OSD([sQuery(id+"F0.wireOp",EDGE,"E1")])]}),"instanceName":"1"}),"instanceName":"1"}),"instanceName":"1"}),"instanceName":"1"}),"instanceName":"1"});
            var Q2595;
            Q2595=makeQuery(id+"F13.opPattern","COPY",BODY,{"derivedFrom":makeQuery(id+"F12.opPattern","COPY",BODY,{"derivedFrom":makeQuery(id+"F10.opPattern","COPY",BODY,{"derivedFrom":makeQuery(id+"F9.opPattern","COPY",BODY,{"derivedFrom":makeQuery(id+"F4.opPattern","COPY",BODY,{"derivedFrom":makeQuery(id+"F2.opPattern","COPY",BODY,{"derivedFrom":makeQuery(id+"F1.opRevolve","SWEPT_BODY",BODY,{"disambiguationData":[OSD([sQuery(id+"F0.wireOp",EDGE,"E1")])]}),"instanceName":"1"}),"instanceName":"1"}),"instanceName":"1"}),"instanceName":"1"}),"instanceName":"1"}),"instanceName":"1"});
            var Q2596;
            Q2596=makeQuery(id+"F13.opPattern","COPY",BODY,{"derivedFrom":makeQuery(id+"F12.opPattern","COPY",BODY,{"derivedFrom":makeQuery(id+"F10.opPattern","COPY",BODY,{"derivedFrom":makeQuery(id+"F9.opPattern","COPY",BODY,{"derivedFrom":makeQuery(id+"F4.opPattern","COPY",BODY,{"derivedFrom":makeQuery(id+"F3.opPattern","COPY",BODY,{"derivedFrom":makeQuery(id+"F2.opPattern","COPY",BODY,{"derivedFrom":makeQuery(id+"F1.opRevolve","SWEPT_BODY",BODY,{"disambiguationData":[OSD([sQuery(id+"F0.wireOp",EDGE,"E1")])]}),"instanceName":"1"}),"instanceName":"1"}),"instanceName":"1"}),"instanceName":"1"}),"instanceName":"1"}),"instanceName":"1"}),"instanceName":"1"});
            var Q2597;
            Q2597=makeQuery(id+"F13.opPattern","COPY",BODY,{"derivedFrom":makeQuery(id+"F12.opPattern","COPY",BODY,{"derivedFrom":makeQuery(id+"F10.opPattern","COPY",BODY,{"derivedFrom":makeQuery(id+"F9.opPattern","COPY",BODY,{"derivedFrom":makeQuery(id+"F5.opPattern","COPY",BODY,{"derivedFrom":makeQuery(id+"F1.opRevolve","SWEPT_BODY",BODY,{"disambiguationData":[OSD([sQuery(id+"F0.wireOp",EDGE,"E1")])]}),"instanceName":"1"}),"instanceName":"1"}),"instanceName":"1"}),"instanceName":"1"}),"instanceName":"1"});
            var Q2598;
            Q2598=makeQuery(id+"F13.opPattern","COPY",BODY,{"derivedFrom":makeQuery(id+"F12.opPattern","COPY",BODY,{"derivedFrom":makeQuery(id+"F10.opPattern","COPY",BODY,{"derivedFrom":makeQuery(id+"F9.opPattern","COPY",BODY,{"derivedFrom":makeQuery(id+"F5.opPattern","COPY",BODY,{"derivedFrom":makeQuery(id+"F2.opPattern","COPY",BODY,{"derivedFrom":makeQuery(id+"F1.opRevolve","SWEPT_BODY",BODY,{"disambiguationData":[OSD([sQuery(id+"F0.wireOp",EDGE,"E1")])]}),"instanceName":"1"}),"instanceName":"1"}),"instanceName":"1"}),"instanceName":"1"}),"instanceName":"1"}),"instanceName":"1"});
            var Q2599;
            Q2599=makeQuery(id+"F13.opPattern","COPY",BODY,{"derivedFrom":makeQuery(id+"F12.opPattern","COPY",BODY,{"derivedFrom":makeQuery(id+"F10.opPattern","COPY",BODY,{"derivedFrom":makeQuery(id+"F9.opPattern","COPY",BODY,{"derivedFrom":makeQuery(id+"F5.opPattern","COPY",BODY,{"derivedFrom":makeQuery(id+"F3.opPattern","COPY",BODY,{"derivedFrom":makeQuery(id+"F2.opPattern","COPY",BODY,{"derivedFrom":makeQuery(id+"F1.opRevolve","SWEPT_BODY",BODY,{"disambiguationData":[OSD([sQuery(id+"F0.wireOp",EDGE,"E1")])]}),"instanceName":"1"}),"instanceName":"1"}),"instanceName":"1"}),"instanceName":"1"}),"instanceName":"1"}),"instanceName":"1"}),"instanceName":"1"});
            var Q2600;
            Q2600=makeQuery(id+"F13.opPattern","COPY",BODY,{"derivedFrom":makeQuery(id+"F12.opPattern","COPY",BODY,{"derivedFrom":makeQuery(id+"F10.opPattern","COPY",BODY,{"derivedFrom":makeQuery(id+"F9.opPattern","COPY",BODY,{"derivedFrom":makeQuery(id+"F5.opPattern","COPY",BODY,{"derivedFrom":makeQuery(id+"F4.opPattern","COPY",BODY,{"derivedFrom":makeQuery(id+"F1.opRevolve","SWEPT_BODY",BODY,{"disambiguationData":[OSD([sQuery(id+"F0.wireOp",EDGE,"E1")])]}),"instanceName":"1"}),"instanceName":"1"}),"instanceName":"1"}),"instanceName":"1"}),"instanceName":"1"}),"instanceName":"1"});
            var Q2601;
            Q2601=makeQuery(id+"F13.opPattern","COPY",BODY,{"derivedFrom":makeQuery(id+"F12.opPattern","COPY",BODY,{"derivedFrom":makeQuery(id+"F10.opPattern","COPY",BODY,{"derivedFrom":makeQuery(id+"F9.opPattern","COPY",BODY,{"derivedFrom":makeQuery(id+"F5.opPattern","COPY",BODY,{"derivedFrom":makeQuery(id+"F4.opPattern","COPY",BODY,{"derivedFrom":makeQuery(id+"F2.opPattern","COPY",BODY,{"derivedFrom":makeQuery(id+"F1.opRevolve","SWEPT_BODY",BODY,{"disambiguationData":[OSD([sQuery(id+"F0.wireOp",EDGE,"E1")])]}),"instanceName":"1"}),"instanceName":"1"}),"instanceName":"1"}),"instanceName":"1"}),"instanceName":"1"}),"instanceName":"1"}),"instanceName":"1"});
            var Q2602;
            Q2602=makeQuery(id+"F13.opPattern","COPY",BODY,{"derivedFrom":makeQuery(id+"F12.opPattern","COPY",BODY,{"derivedFrom":makeQuery(id+"F10.opPattern","COPY",BODY,{"derivedFrom":makeQuery(id+"F9.opPattern","COPY",BODY,{"derivedFrom":makeQuery(id+"F5.opPattern","COPY",BODY,{"derivedFrom":makeQuery(id+"F4.opPattern","COPY",BODY,{"derivedFrom":makeQuery(id+"F3.opPattern","COPY",BODY,{"derivedFrom":makeQuery(id+"F2.opPattern","COPY",BODY,{"derivedFrom":makeQuery(id+"F1.opRevolve","SWEPT_BODY",BODY,{"disambiguationData":[OSD([sQuery(id+"F0.wireOp",EDGE,"E1")])]}),"instanceName":"1"}),"instanceName":"1"}),"instanceName":"1"}),"instanceName":"1"}),"instanceName":"1"}),"instanceName":"1"}),"instanceName":"1"}),"instanceName":"1"});
            var Q2603;
            Q2603=makeQuery(id+"F13.opPattern","COPY",BODY,{"derivedFrom":makeQuery(id+"F12.opPattern","COPY",BODY,{"derivedFrom":makeQuery(id+"F10.opPattern","COPY",BODY,{"derivedFrom":makeQuery(id+"F9.opPattern","COPY",BODY,{"derivedFrom":makeQuery(id+"F6.opPattern","COPY",BODY,{"derivedFrom":makeQuery(id+"F1.opRevolve","SWEPT_BODY",BODY,{"disambiguationData":[OSD([sQuery(id+"F0.wireOp",EDGE,"E1")])]}),"instanceName":"1"}),"instanceName":"1"}),"instanceName":"1"}),"instanceName":"1"}),"instanceName":"1"});
            var Q2604;
            Q2604=makeQuery(id+"F13.opPattern","COPY",BODY,{"derivedFrom":makeQuery(id+"F12.opPattern","COPY",BODY,{"derivedFrom":makeQuery(id+"F10.opPattern","COPY",BODY,{"derivedFrom":makeQuery(id+"F9.opPattern","COPY",BODY,{"derivedFrom":makeQuery(id+"F6.opPattern","COPY",BODY,{"derivedFrom":makeQuery(id+"F2.opPattern","COPY",BODY,{"derivedFrom":makeQuery(id+"F1.opRevolve","SWEPT_BODY",BODY,{"disambiguationData":[OSD([sQuery(id+"F0.wireOp",EDGE,"E1")])]}),"instanceName":"1"}),"instanceName":"1"}),"instanceName":"1"}),"instanceName":"1"}),"instanceName":"1"}),"instanceName":"1"});
            var Q2605;
            Q2605=makeQuery(id+"F13.opPattern","COPY",BODY,{"derivedFrom":makeQuery(id+"F12.opPattern","COPY",BODY,{"derivedFrom":makeQuery(id+"F10.opPattern","COPY",BODY,{"derivedFrom":makeQuery(id+"F9.opPattern","COPY",BODY,{"derivedFrom":makeQuery(id+"F6.opPattern","COPY",BODY,{"derivedFrom":makeQuery(id+"F3.opPattern","COPY",BODY,{"derivedFrom":makeQuery(id+"F2.opPattern","COPY",BODY,{"derivedFrom":makeQuery(id+"F1.opRevolve","SWEPT_BODY",BODY,{"disambiguationData":[OSD([sQuery(id+"F0.wireOp",EDGE,"E1")])]}),"instanceName":"1"}),"instanceName":"1"}),"instanceName":"1"}),"instanceName":"1"}),"instanceName":"1"}),"instanceName":"1"}),"instanceName":"1"});
            var Q2606;
            Q2606=makeQuery(id+"F13.opPattern","COPY",BODY,{"derivedFrom":makeQuery(id+"F12.opPattern","COPY",BODY,{"derivedFrom":makeQuery(id+"F10.opPattern","COPY",BODY,{"derivedFrom":makeQuery(id+"F9.opPattern","COPY",BODY,{"derivedFrom":makeQuery(id+"F6.opPattern","COPY",BODY,{"derivedFrom":makeQuery(id+"F4.opPattern","COPY",BODY,{"derivedFrom":makeQuery(id+"F1.opRevolve","SWEPT_BODY",BODY,{"disambiguationData":[OSD([sQuery(id+"F0.wireOp",EDGE,"E1")])]}),"instanceName":"1"}),"instanceName":"1"}),"instanceName":"1"}),"instanceName":"1"}),"instanceName":"1"}),"instanceName":"1"});
            var Q2607;
            Q2607=makeQuery(id+"F13.opPattern","COPY",BODY,{"derivedFrom":makeQuery(id+"F12.opPattern","COPY",BODY,{"derivedFrom":makeQuery(id+"F10.opPattern","COPY",BODY,{"derivedFrom":makeQuery(id+"F9.opPattern","COPY",BODY,{"derivedFrom":makeQuery(id+"F6.opPattern","COPY",BODY,{"derivedFrom":makeQuery(id+"F4.opPattern","COPY",BODY,{"derivedFrom":makeQuery(id+"F2.opPattern","COPY",BODY,{"derivedFrom":makeQuery(id+"F1.opRevolve","SWEPT_BODY",BODY,{"disambiguationData":[OSD([sQuery(id+"F0.wireOp",EDGE,"E1")])]}),"instanceName":"1"}),"instanceName":"1"}),"instanceName":"1"}),"instanceName":"1"}),"instanceName":"1"}),"instanceName":"1"}),"instanceName":"1"});
            var Q2608;
            Q2608=makeQuery(id+"F13.opPattern","COPY",BODY,{"derivedFrom":makeQuery(id+"F12.opPattern","COPY",BODY,{"derivedFrom":makeQuery(id+"F10.opPattern","COPY",BODY,{"derivedFrom":makeQuery(id+"F9.opPattern","COPY",BODY,{"derivedFrom":makeQuery(id+"F6.opPattern","COPY",BODY,{"derivedFrom":makeQuery(id+"F4.opPattern","COPY",BODY,{"derivedFrom":makeQuery(id+"F3.opPattern","COPY",BODY,{"derivedFrom":makeQuery(id+"F2.opPattern","COPY",BODY,{"derivedFrom":makeQuery(id+"F1.opRevolve","SWEPT_BODY",BODY,{"disambiguationData":[OSD([sQuery(id+"F0.wireOp",EDGE,"E1")])]}),"instanceName":"1"}),"instanceName":"1"}),"instanceName":"1"}),"instanceName":"1"}),"instanceName":"1"}),"instanceName":"1"}),"instanceName":"1"}),"instanceName":"1"});
            var Q2609;
            Q2609=makeQuery(id+"F13.opPattern","COPY",BODY,{"derivedFrom":makeQuery(id+"F12.opPattern","COPY",BODY,{"derivedFrom":makeQuery(id+"F10.opPattern","COPY",BODY,{"derivedFrom":makeQuery(id+"F9.opPattern","COPY",BODY,{"derivedFrom":makeQuery(id+"F6.opPattern","COPY",BODY,{"derivedFrom":makeQuery(id+"F5.opPattern","COPY",BODY,{"derivedFrom":makeQuery(id+"F1.opRevolve","SWEPT_BODY",BODY,{"disambiguationData":[OSD([sQuery(id+"F0.wireOp",EDGE,"E1")])]}),"instanceName":"1"}),"instanceName":"1"}),"instanceName":"1"}),"instanceName":"1"}),"instanceName":"1"}),"instanceName":"1"});
            var Q2610;
            Q2610=makeQuery(id+"F13.opPattern","COPY",BODY,{"derivedFrom":makeQuery(id+"F12.opPattern","COPY",BODY,{"derivedFrom":makeQuery(id+"F10.opPattern","COPY",BODY,{"derivedFrom":makeQuery(id+"F9.opPattern","COPY",BODY,{"derivedFrom":makeQuery(id+"F6.opPattern","COPY",BODY,{"derivedFrom":makeQuery(id+"F5.opPattern","COPY",BODY,{"derivedFrom":makeQuery(id+"F2.opPattern","COPY",BODY,{"derivedFrom":makeQuery(id+"F1.opRevolve","SWEPT_BODY",BODY,{"disambiguationData":[OSD([sQuery(id+"F0.wireOp",EDGE,"E1")])]}),"instanceName":"1"}),"instanceName":"1"}),"instanceName":"1"}),"instanceName":"1"}),"instanceName":"1"}),"instanceName":"1"}),"instanceName":"1"});
            var Q2611;
            Q2611=makeQuery(id+"F13.opPattern","COPY",BODY,{"derivedFrom":makeQuery(id+"F12.opPattern","COPY",BODY,{"derivedFrom":makeQuery(id+"F10.opPattern","COPY",BODY,{"derivedFrom":makeQuery(id+"F9.opPattern","COPY",BODY,{"derivedFrom":makeQuery(id+"F6.opPattern","COPY",BODY,{"derivedFrom":makeQuery(id+"F5.opPattern","COPY",BODY,{"derivedFrom":makeQuery(id+"F3.opPattern","COPY",BODY,{"derivedFrom":makeQuery(id+"F2.opPattern","COPY",BODY,{"derivedFrom":makeQuery(id+"F1.opRevolve","SWEPT_BODY",BODY,{"disambiguationData":[OSD([sQuery(id+"F0.wireOp",EDGE,"E1")])]}),"instanceName":"1"}),"instanceName":"1"}),"instanceName":"1"}),"instanceName":"1"}),"instanceName":"1"}),"instanceName":"1"}),"instanceName":"1"}),"instanceName":"1"});
            var Q2612;
            Q2612=makeQuery(id+"F13.opPattern","COPY",BODY,{"derivedFrom":makeQuery(id+"F12.opPattern","COPY",BODY,{"derivedFrom":makeQuery(id+"F10.opPattern","COPY",BODY,{"derivedFrom":makeQuery(id+"F9.opPattern","COPY",BODY,{"derivedFrom":makeQuery(id+"F6.opPattern","COPY",BODY,{"derivedFrom":makeQuery(id+"F5.opPattern","COPY",BODY,{"derivedFrom":makeQuery(id+"F4.opPattern","COPY",BODY,{"derivedFrom":makeQuery(id+"F1.opRevolve","SWEPT_BODY",BODY,{"disambiguationData":[OSD([sQuery(id+"F0.wireOp",EDGE,"E1")])]}),"instanceName":"1"}),"instanceName":"1"}),"instanceName":"1"}),"instanceName":"1"}),"instanceName":"1"}),"instanceName":"1"}),"instanceName":"1"});
            var Q2613;
            Q2613=makeQuery(id+"F13.opPattern","COPY",BODY,{"derivedFrom":makeQuery(id+"F12.opPattern","COPY",BODY,{"derivedFrom":makeQuery(id+"F10.opPattern","COPY",BODY,{"derivedFrom":makeQuery(id+"F9.opPattern","COPY",BODY,{"derivedFrom":makeQuery(id+"F6.opPattern","COPY",BODY,{"derivedFrom":makeQuery(id+"F5.opPattern","COPY",BODY,{"derivedFrom":makeQuery(id+"F4.opPattern","COPY",BODY,{"derivedFrom":makeQuery(id+"F2.opPattern","COPY",BODY,{"derivedFrom":makeQuery(id+"F1.opRevolve","SWEPT_BODY",BODY,{"disambiguationData":[OSD([sQuery(id+"F0.wireOp",EDGE,"E1")])]}),"instanceName":"1"}),"instanceName":"1"}),"instanceName":"1"}),"instanceName":"1"}),"instanceName":"1"}),"instanceName":"1"}),"instanceName":"1"}),"instanceName":"1"});
            var Q2614;
            Q2614=makeQuery(id+"F13.opPattern","COPY",BODY,{"derivedFrom":makeQuery(id+"F12.opPattern","COPY",BODY,{"derivedFrom":makeQuery(id+"F10.opPattern","COPY",BODY,{"derivedFrom":makeQuery(id+"F9.opPattern","COPY",BODY,{"derivedFrom":makeQuery(id+"F6.opPattern","COPY",BODY,{"derivedFrom":makeQuery(id+"F5.opPattern","COPY",BODY,{"derivedFrom":makeQuery(id+"F4.opPattern","COPY",BODY,{"derivedFrom":makeQuery(id+"F3.opPattern","COPY",BODY,{"derivedFrom":makeQuery(id+"F2.opPattern","COPY",BODY,{"derivedFrom":makeQuery(id+"F1.opRevolve","SWEPT_BODY",BODY,{"disambiguationData":[OSD([sQuery(id+"F0.wireOp",EDGE,"E1")])]}),"instanceName":"1"}),"instanceName":"1"}),"instanceName":"1"}),"instanceName":"1"}),"instanceName":"1"}),"instanceName":"1"}),"instanceName":"1"}),"instanceName":"1"}),"instanceName":"1"});
            var Q2615;
            Q2615=makeQuery(id+"F13.opPattern","COPY",BODY,{"derivedFrom":makeQuery(id+"F12.opPattern","COPY",BODY,{"derivedFrom":makeQuery(id+"F10.opPattern","COPY",BODY,{"derivedFrom":makeQuery(id+"F9.opPattern","COPY",BODY,{"derivedFrom":makeQuery(id+"F7.opPattern","COPY",BODY,{"derivedFrom":makeQuery(id+"F1.opRevolve","SWEPT_BODY",BODY,{"disambiguationData":[OSD([sQuery(id+"F0.wireOp",EDGE,"E1")])]}),"instanceName":"1"}),"instanceName":"1"}),"instanceName":"1"}),"instanceName":"1"}),"instanceName":"1"});
            var Q2616;
            Q2616=makeQuery(id+"F13.opPattern","COPY",BODY,{"derivedFrom":makeQuery(id+"F12.opPattern","COPY",BODY,{"derivedFrom":makeQuery(id+"F10.opPattern","COPY",BODY,{"derivedFrom":makeQuery(id+"F9.opPattern","COPY",BODY,{"derivedFrom":makeQuery(id+"F7.opPattern","COPY",BODY,{"derivedFrom":makeQuery(id+"F2.opPattern","COPY",BODY,{"derivedFrom":makeQuery(id+"F1.opRevolve","SWEPT_BODY",BODY,{"disambiguationData":[OSD([sQuery(id+"F0.wireOp",EDGE,"E1")])]}),"instanceName":"1"}),"instanceName":"1"}),"instanceName":"1"}),"instanceName":"1"}),"instanceName":"1"}),"instanceName":"1"});
            var Q2617;
            Q2617=makeQuery(id+"F13.opPattern","COPY",BODY,{"derivedFrom":makeQuery(id+"F12.opPattern","COPY",BODY,{"derivedFrom":makeQuery(id+"F10.opPattern","COPY",BODY,{"derivedFrom":makeQuery(id+"F9.opPattern","COPY",BODY,{"derivedFrom":makeQuery(id+"F7.opPattern","COPY",BODY,{"derivedFrom":makeQuery(id+"F3.opPattern","COPY",BODY,{"derivedFrom":makeQuery(id+"F2.opPattern","COPY",BODY,{"derivedFrom":makeQuery(id+"F1.opRevolve","SWEPT_BODY",BODY,{"disambiguationData":[OSD([sQuery(id+"F0.wireOp",EDGE,"E1")])]}),"instanceName":"1"}),"instanceName":"1"}),"instanceName":"1"}),"instanceName":"1"}),"instanceName":"1"}),"instanceName":"1"}),"instanceName":"1"});
            var Q2618;
            Q2618=makeQuery(id+"F13.opPattern","COPY",BODY,{"derivedFrom":makeQuery(id+"F12.opPattern","COPY",BODY,{"derivedFrom":makeQuery(id+"F10.opPattern","COPY",BODY,{"derivedFrom":makeQuery(id+"F9.opPattern","COPY",BODY,{"derivedFrom":makeQuery(id+"F7.opPattern","COPY",BODY,{"derivedFrom":makeQuery(id+"F4.opPattern","COPY",BODY,{"derivedFrom":makeQuery(id+"F1.opRevolve","SWEPT_BODY",BODY,{"disambiguationData":[OSD([sQuery(id+"F0.wireOp",EDGE,"E1")])]}),"instanceName":"1"}),"instanceName":"1"}),"instanceName":"1"}),"instanceName":"1"}),"instanceName":"1"}),"instanceName":"1"});
            var Q2619;
            Q2619=makeQuery(id+"F13.opPattern","COPY",BODY,{"derivedFrom":makeQuery(id+"F12.opPattern","COPY",BODY,{"derivedFrom":makeQuery(id+"F10.opPattern","COPY",BODY,{"derivedFrom":makeQuery(id+"F9.opPattern","COPY",BODY,{"derivedFrom":makeQuery(id+"F7.opPattern","COPY",BODY,{"derivedFrom":makeQuery(id+"F4.opPattern","COPY",BODY,{"derivedFrom":makeQuery(id+"F2.opPattern","COPY",BODY,{"derivedFrom":makeQuery(id+"F1.opRevolve","SWEPT_BODY",BODY,{"disambiguationData":[OSD([sQuery(id+"F0.wireOp",EDGE,"E1")])]}),"instanceName":"1"}),"instanceName":"1"}),"instanceName":"1"}),"instanceName":"1"}),"instanceName":"1"}),"instanceName":"1"}),"instanceName":"1"});
            var Q2620;
            Q2620=makeQuery(id+"F13.opPattern","COPY",BODY,{"derivedFrom":makeQuery(id+"F12.opPattern","COPY",BODY,{"derivedFrom":makeQuery(id+"F10.opPattern","COPY",BODY,{"derivedFrom":makeQuery(id+"F9.opPattern","COPY",BODY,{"derivedFrom":makeQuery(id+"F7.opPattern","COPY",BODY,{"derivedFrom":makeQuery(id+"F4.opPattern","COPY",BODY,{"derivedFrom":makeQuery(id+"F3.opPattern","COPY",BODY,{"derivedFrom":makeQuery(id+"F2.opPattern","COPY",BODY,{"derivedFrom":makeQuery(id+"F1.opRevolve","SWEPT_BODY",BODY,{"disambiguationData":[OSD([sQuery(id+"F0.wireOp",EDGE,"E1")])]}),"instanceName":"1"}),"instanceName":"1"}),"instanceName":"1"}),"instanceName":"1"}),"instanceName":"1"}),"instanceName":"1"}),"instanceName":"1"}),"instanceName":"1"});
            var Q2621;
            Q2621=makeQuery(id+"F13.opPattern","COPY",BODY,{"derivedFrom":makeQuery(id+"F12.opPattern","COPY",BODY,{"derivedFrom":makeQuery(id+"F10.opPattern","COPY",BODY,{"derivedFrom":makeQuery(id+"F9.opPattern","COPY",BODY,{"derivedFrom":makeQuery(id+"F7.opPattern","COPY",BODY,{"derivedFrom":makeQuery(id+"F5.opPattern","COPY",BODY,{"derivedFrom":makeQuery(id+"F1.opRevolve","SWEPT_BODY",BODY,{"disambiguationData":[OSD([sQuery(id+"F0.wireOp",EDGE,"E1")])]}),"instanceName":"1"}),"instanceName":"1"}),"instanceName":"1"}),"instanceName":"1"}),"instanceName":"1"}),"instanceName":"1"});
            var Q2622;
            Q2622=makeQuery(id+"F13.opPattern","COPY",BODY,{"derivedFrom":makeQuery(id+"F12.opPattern","COPY",BODY,{"derivedFrom":makeQuery(id+"F10.opPattern","COPY",BODY,{"derivedFrom":makeQuery(id+"F9.opPattern","COPY",BODY,{"derivedFrom":makeQuery(id+"F7.opPattern","COPY",BODY,{"derivedFrom":makeQuery(id+"F5.opPattern","COPY",BODY,{"derivedFrom":makeQuery(id+"F2.opPattern","COPY",BODY,{"derivedFrom":makeQuery(id+"F1.opRevolve","SWEPT_BODY",BODY,{"disambiguationData":[OSD([sQuery(id+"F0.wireOp",EDGE,"E1")])]}),"instanceName":"1"}),"instanceName":"1"}),"instanceName":"1"}),"instanceName":"1"}),"instanceName":"1"}),"instanceName":"1"}),"instanceName":"1"});
            var Q2623;
            Q2623=makeQuery(id+"F13.opPattern","COPY",BODY,{"derivedFrom":makeQuery(id+"F12.opPattern","COPY",BODY,{"derivedFrom":makeQuery(id+"F10.opPattern","COPY",BODY,{"derivedFrom":makeQuery(id+"F9.opPattern","COPY",BODY,{"derivedFrom":makeQuery(id+"F7.opPattern","COPY",BODY,{"derivedFrom":makeQuery(id+"F5.opPattern","COPY",BODY,{"derivedFrom":makeQuery(id+"F3.opPattern","COPY",BODY,{"derivedFrom":makeQuery(id+"F2.opPattern","COPY",BODY,{"derivedFrom":makeQuery(id+"F1.opRevolve","SWEPT_BODY",BODY,{"disambiguationData":[OSD([sQuery(id+"F0.wireOp",EDGE,"E1")])]}),"instanceName":"1"}),"instanceName":"1"}),"instanceName":"1"}),"instanceName":"1"}),"instanceName":"1"}),"instanceName":"1"}),"instanceName":"1"}),"instanceName":"1"});
            var Q2624;
            Q2624=makeQuery(id+"F13.opPattern","COPY",BODY,{"derivedFrom":makeQuery(id+"F12.opPattern","COPY",BODY,{"derivedFrom":makeQuery(id+"F10.opPattern","COPY",BODY,{"derivedFrom":makeQuery(id+"F9.opPattern","COPY",BODY,{"derivedFrom":makeQuery(id+"F7.opPattern","COPY",BODY,{"derivedFrom":makeQuery(id+"F5.opPattern","COPY",BODY,{"derivedFrom":makeQuery(id+"F4.opPattern","COPY",BODY,{"derivedFrom":makeQuery(id+"F1.opRevolve","SWEPT_BODY",BODY,{"disambiguationData":[OSD([sQuery(id+"F0.wireOp",EDGE,"E1")])]}),"instanceName":"1"}),"instanceName":"1"}),"instanceName":"1"}),"instanceName":"1"}),"instanceName":"1"}),"instanceName":"1"}),"instanceName":"1"});
            var Q2625;
            Q2625=makeQuery(id+"F13.opPattern","COPY",BODY,{"derivedFrom":makeQuery(id+"F12.opPattern","COPY",BODY,{"derivedFrom":makeQuery(id+"F10.opPattern","COPY",BODY,{"derivedFrom":makeQuery(id+"F9.opPattern","COPY",BODY,{"derivedFrom":makeQuery(id+"F7.opPattern","COPY",BODY,{"derivedFrom":makeQuery(id+"F5.opPattern","COPY",BODY,{"derivedFrom":makeQuery(id+"F4.opPattern","COPY",BODY,{"derivedFrom":makeQuery(id+"F2.opPattern","COPY",BODY,{"derivedFrom":makeQuery(id+"F1.opRevolve","SWEPT_BODY",BODY,{"disambiguationData":[OSD([sQuery(id+"F0.wireOp",EDGE,"E1")])]}),"instanceName":"1"}),"instanceName":"1"}),"instanceName":"1"}),"instanceName":"1"}),"instanceName":"1"}),"instanceName":"1"}),"instanceName":"1"}),"instanceName":"1"});
            var Q2626;
            Q2626=makeQuery(id+"F13.opPattern","COPY",BODY,{"derivedFrom":makeQuery(id+"F12.opPattern","COPY",BODY,{"derivedFrom":makeQuery(id+"F10.opPattern","COPY",BODY,{"derivedFrom":makeQuery(id+"F9.opPattern","COPY",BODY,{"derivedFrom":makeQuery(id+"F7.opPattern","COPY",BODY,{"derivedFrom":makeQuery(id+"F5.opPattern","COPY",BODY,{"derivedFrom":makeQuery(id+"F4.opPattern","COPY",BODY,{"derivedFrom":makeQuery(id+"F3.opPattern","COPY",BODY,{"derivedFrom":makeQuery(id+"F2.opPattern","COPY",BODY,{"derivedFrom":makeQuery(id+"F1.opRevolve","SWEPT_BODY",BODY,{"disambiguationData":[OSD([sQuery(id+"F0.wireOp",EDGE,"E1")])]}),"instanceName":"1"}),"instanceName":"1"}),"instanceName":"1"}),"instanceName":"1"}),"instanceName":"1"}),"instanceName":"1"}),"instanceName":"1"}),"instanceName":"1"}),"instanceName":"1"});
            var Q2627;
            Q2627=makeQuery(id+"F13.opPattern","COPY",BODY,{"derivedFrom":makeQuery(id+"F12.opPattern","COPY",BODY,{"derivedFrom":makeQuery(id+"F10.opPattern","COPY",BODY,{"derivedFrom":makeQuery(id+"F9.opPattern","COPY",BODY,{"derivedFrom":makeQuery(id+"F7.opPattern","COPY",BODY,{"derivedFrom":makeQuery(id+"F6.opPattern","COPY",BODY,{"derivedFrom":makeQuery(id+"F1.opRevolve","SWEPT_BODY",BODY,{"disambiguationData":[OSD([sQuery(id+"F0.wireOp",EDGE,"E1")])]}),"instanceName":"1"}),"instanceName":"1"}),"instanceName":"1"}),"instanceName":"1"}),"instanceName":"1"}),"instanceName":"1"});
            var Q2628;
            Q2628=makeQuery(id+"F13.opPattern","COPY",BODY,{"derivedFrom":makeQuery(id+"F12.opPattern","COPY",BODY,{"derivedFrom":makeQuery(id+"F10.opPattern","COPY",BODY,{"derivedFrom":makeQuery(id+"F9.opPattern","COPY",BODY,{"derivedFrom":makeQuery(id+"F7.opPattern","COPY",BODY,{"derivedFrom":makeQuery(id+"F6.opPattern","COPY",BODY,{"derivedFrom":makeQuery(id+"F2.opPattern","COPY",BODY,{"derivedFrom":makeQuery(id+"F1.opRevolve","SWEPT_BODY",BODY,{"disambiguationData":[OSD([sQuery(id+"F0.wireOp",EDGE,"E1")])]}),"instanceName":"1"}),"instanceName":"1"}),"instanceName":"1"}),"instanceName":"1"}),"instanceName":"1"}),"instanceName":"1"}),"instanceName":"1"});
            var Q2629;
            Q2629=makeQuery(id+"F13.opPattern","COPY",BODY,{"derivedFrom":makeQuery(id+"F12.opPattern","COPY",BODY,{"derivedFrom":makeQuery(id+"F10.opPattern","COPY",BODY,{"derivedFrom":makeQuery(id+"F9.opPattern","COPY",BODY,{"derivedFrom":makeQuery(id+"F7.opPattern","COPY",BODY,{"derivedFrom":makeQuery(id+"F6.opPattern","COPY",BODY,{"derivedFrom":makeQuery(id+"F3.opPattern","COPY",BODY,{"derivedFrom":makeQuery(id+"F2.opPattern","COPY",BODY,{"derivedFrom":makeQuery(id+"F1.opRevolve","SWEPT_BODY",BODY,{"disambiguationData":[OSD([sQuery(id+"F0.wireOp",EDGE,"E1")])]}),"instanceName":"1"}),"instanceName":"1"}),"instanceName":"1"}),"instanceName":"1"}),"instanceName":"1"}),"instanceName":"1"}),"instanceName":"1"}),"instanceName":"1"});
            var Q2630;
            Q2630=makeQuery(id+"F13.opPattern","COPY",BODY,{"derivedFrom":makeQuery(id+"F12.opPattern","COPY",BODY,{"derivedFrom":makeQuery(id+"F10.opPattern","COPY",BODY,{"derivedFrom":makeQuery(id+"F9.opPattern","COPY",BODY,{"derivedFrom":makeQuery(id+"F7.opPattern","COPY",BODY,{"derivedFrom":makeQuery(id+"F6.opPattern","COPY",BODY,{"derivedFrom":makeQuery(id+"F4.opPattern","COPY",BODY,{"derivedFrom":makeQuery(id+"F1.opRevolve","SWEPT_BODY",BODY,{"disambiguationData":[OSD([sQuery(id+"F0.wireOp",EDGE,"E1")])]}),"instanceName":"1"}),"instanceName":"1"}),"instanceName":"1"}),"instanceName":"1"}),"instanceName":"1"}),"instanceName":"1"}),"instanceName":"1"});
            var Q2631;
            Q2631=makeQuery(id+"F13.opPattern","COPY",BODY,{"derivedFrom":makeQuery(id+"F12.opPattern","COPY",BODY,{"derivedFrom":makeQuery(id+"F10.opPattern","COPY",BODY,{"derivedFrom":makeQuery(id+"F9.opPattern","COPY",BODY,{"derivedFrom":makeQuery(id+"F7.opPattern","COPY",BODY,{"derivedFrom":makeQuery(id+"F6.opPattern","COPY",BODY,{"derivedFrom":makeQuery(id+"F4.opPattern","COPY",BODY,{"derivedFrom":makeQuery(id+"F2.opPattern","COPY",BODY,{"derivedFrom":makeQuery(id+"F1.opRevolve","SWEPT_BODY",BODY,{"disambiguationData":[OSD([sQuery(id+"F0.wireOp",EDGE,"E1")])]}),"instanceName":"1"}),"instanceName":"1"}),"instanceName":"1"}),"instanceName":"1"}),"instanceName":"1"}),"instanceName":"1"}),"instanceName":"1"}),"instanceName":"1"});
            var Q2632;
            Q2632=makeQuery(id+"F13.opPattern","COPY",BODY,{"derivedFrom":makeQuery(id+"F12.opPattern","COPY",BODY,{"derivedFrom":makeQuery(id+"F10.opPattern","COPY",BODY,{"derivedFrom":makeQuery(id+"F9.opPattern","COPY",BODY,{"derivedFrom":makeQuery(id+"F7.opPattern","COPY",BODY,{"derivedFrom":makeQuery(id+"F6.opPattern","COPY",BODY,{"derivedFrom":makeQuery(id+"F4.opPattern","COPY",BODY,{"derivedFrom":makeQuery(id+"F3.opPattern","COPY",BODY,{"derivedFrom":makeQuery(id+"F2.opPattern","COPY",BODY,{"derivedFrom":makeQuery(id+"F1.opRevolve","SWEPT_BODY",BODY,{"disambiguationData":[OSD([sQuery(id+"F0.wireOp",EDGE,"E1")])]}),"instanceName":"1"}),"instanceName":"1"}),"instanceName":"1"}),"instanceName":"1"}),"instanceName":"1"}),"instanceName":"1"}),"instanceName":"1"}),"instanceName":"1"}),"instanceName":"1"});
            var Q2633;
            Q2633=makeQuery(id+"F13.opPattern","COPY",BODY,{"derivedFrom":makeQuery(id+"F12.opPattern","COPY",BODY,{"derivedFrom":makeQuery(id+"F10.opPattern","COPY",BODY,{"derivedFrom":makeQuery(id+"F9.opPattern","COPY",BODY,{"derivedFrom":makeQuery(id+"F7.opPattern","COPY",BODY,{"derivedFrom":makeQuery(id+"F6.opPattern","COPY",BODY,{"derivedFrom":makeQuery(id+"F5.opPattern","COPY",BODY,{"derivedFrom":makeQuery(id+"F1.opRevolve","SWEPT_BODY",BODY,{"disambiguationData":[OSD([sQuery(id+"F0.wireOp",EDGE,"E1")])]}),"instanceName":"1"}),"instanceName":"1"}),"instanceName":"1"}),"instanceName":"1"}),"instanceName":"1"}),"instanceName":"1"}),"instanceName":"1"});
            var Q2634;
            Q2634=makeQuery(id+"F13.opPattern","COPY",BODY,{"derivedFrom":makeQuery(id+"F12.opPattern","COPY",BODY,{"derivedFrom":makeQuery(id+"F10.opPattern","COPY",BODY,{"derivedFrom":makeQuery(id+"F9.opPattern","COPY",BODY,{"derivedFrom":makeQuery(id+"F7.opPattern","COPY",BODY,{"derivedFrom":makeQuery(id+"F6.opPattern","COPY",BODY,{"derivedFrom":makeQuery(id+"F5.opPattern","COPY",BODY,{"derivedFrom":makeQuery(id+"F2.opPattern","COPY",BODY,{"derivedFrom":makeQuery(id+"F1.opRevolve","SWEPT_BODY",BODY,{"disambiguationData":[OSD([sQuery(id+"F0.wireOp",EDGE,"E1")])]}),"instanceName":"1"}),"instanceName":"1"}),"instanceName":"1"}),"instanceName":"1"}),"instanceName":"1"}),"instanceName":"1"}),"instanceName":"1"}),"instanceName":"1"});
            var Q2635;
            Q2635=makeQuery(id+"F13.opPattern","COPY",BODY,{"derivedFrom":makeQuery(id+"F12.opPattern","COPY",BODY,{"derivedFrom":makeQuery(id+"F10.opPattern","COPY",BODY,{"derivedFrom":makeQuery(id+"F9.opPattern","COPY",BODY,{"derivedFrom":makeQuery(id+"F7.opPattern","COPY",BODY,{"derivedFrom":makeQuery(id+"F6.opPattern","COPY",BODY,{"derivedFrom":makeQuery(id+"F5.opPattern","COPY",BODY,{"derivedFrom":makeQuery(id+"F3.opPattern","COPY",BODY,{"derivedFrom":makeQuery(id+"F2.opPattern","COPY",BODY,{"derivedFrom":makeQuery(id+"F1.opRevolve","SWEPT_BODY",BODY,{"disambiguationData":[OSD([sQuery(id+"F0.wireOp",EDGE,"E1")])]}),"instanceName":"1"}),"instanceName":"1"}),"instanceName":"1"}),"instanceName":"1"}),"instanceName":"1"}),"instanceName":"1"}),"instanceName":"1"}),"instanceName":"1"}),"instanceName":"1"});
            var Q2636;
            Q2636=makeQuery(id+"F13.opPattern","COPY",BODY,{"derivedFrom":makeQuery(id+"F12.opPattern","COPY",BODY,{"derivedFrom":makeQuery(id+"F10.opPattern","COPY",BODY,{"derivedFrom":makeQuery(id+"F9.opPattern","COPY",BODY,{"derivedFrom":makeQuery(id+"F7.opPattern","COPY",BODY,{"derivedFrom":makeQuery(id+"F6.opPattern","COPY",BODY,{"derivedFrom":makeQuery(id+"F5.opPattern","COPY",BODY,{"derivedFrom":makeQuery(id+"F4.opPattern","COPY",BODY,{"derivedFrom":makeQuery(id+"F1.opRevolve","SWEPT_BODY",BODY,{"disambiguationData":[OSD([sQuery(id+"F0.wireOp",EDGE,"E1")])]}),"instanceName":"1"}),"instanceName":"1"}),"instanceName":"1"}),"instanceName":"1"}),"instanceName":"1"}),"instanceName":"1"}),"instanceName":"1"}),"instanceName":"1"});
            var Q2637;
            Q2637=makeQuery(id+"F13.opPattern","COPY",BODY,{"derivedFrom":makeQuery(id+"F12.opPattern","COPY",BODY,{"derivedFrom":makeQuery(id+"F10.opPattern","COPY",BODY,{"derivedFrom":makeQuery(id+"F9.opPattern","COPY",BODY,{"derivedFrom":makeQuery(id+"F7.opPattern","COPY",BODY,{"derivedFrom":makeQuery(id+"F6.opPattern","COPY",BODY,{"derivedFrom":makeQuery(id+"F5.opPattern","COPY",BODY,{"derivedFrom":makeQuery(id+"F4.opPattern","COPY",BODY,{"derivedFrom":makeQuery(id+"F2.opPattern","COPY",BODY,{"derivedFrom":makeQuery(id+"F1.opRevolve","SWEPT_BODY",BODY,{"disambiguationData":[OSD([sQuery(id+"F0.wireOp",EDGE,"E1")])]}),"instanceName":"1"}),"instanceName":"1"}),"instanceName":"1"}),"instanceName":"1"}),"instanceName":"1"}),"instanceName":"1"}),"instanceName":"1"}),"instanceName":"1"}),"instanceName":"1"});
            var Q2638;
            Q2638=makeQuery(id+"F13.opPattern","COPY",BODY,{"derivedFrom":makeQuery(id+"F12.opPattern","COPY",BODY,{"derivedFrom":makeQuery(id+"F10.opPattern","COPY",BODY,{"derivedFrom":makeQuery(id+"F9.opPattern","COPY",BODY,{"derivedFrom":makeQuery(id+"F7.opPattern","COPY",BODY,{"derivedFrom":makeQuery(id+"F6.opPattern","COPY",BODY,{"derivedFrom":makeQuery(id+"F5.opPattern","COPY",BODY,{"derivedFrom":makeQuery(id+"F4.opPattern","COPY",BODY,{"derivedFrom":makeQuery(id+"F3.opPattern","COPY",BODY,{"derivedFrom":makeQuery(id+"F2.opPattern","COPY",BODY,{"derivedFrom":makeQuery(id+"F1.opRevolve","SWEPT_BODY",BODY,{"disambiguationData":[OSD([sQuery(id+"F0.wireOp",EDGE,"E1")])]}),"instanceName":"1"}),"instanceName":"1"}),"instanceName":"1"}),"instanceName":"1"}),"instanceName":"1"}),"instanceName":"1"}),"instanceName":"1"}),"instanceName":"1"}),"instanceName":"1"}),"instanceName":"1"});
            var Q2639;
            Q2639=makeQuery(id+"F13.opPattern","COPY",BODY,{"derivedFrom":makeQuery(id+"F12.opPattern","COPY",BODY,{"derivedFrom":makeQuery(id+"F10.opPattern","COPY",BODY,{"derivedFrom":makeQuery(id+"F9.opPattern","COPY",BODY,{"derivedFrom":makeQuery(id+"F8.opPattern","COPY",BODY,{"derivedFrom":makeQuery(id+"F1.opRevolve","SWEPT_BODY",BODY,{"disambiguationData":[OSD([sQuery(id+"F0.wireOp",EDGE,"E1")])]}),"instanceName":"1"}),"instanceName":"1"}),"instanceName":"1"}),"instanceName":"1"}),"instanceName":"1"});
            var Q2640;
            Q2640=makeQuery(id+"F13.opPattern","COPY",BODY,{"derivedFrom":makeQuery(id+"F12.opPattern","COPY",BODY,{"derivedFrom":makeQuery(id+"F10.opPattern","COPY",BODY,{"derivedFrom":makeQuery(id+"F9.opPattern","COPY",BODY,{"derivedFrom":makeQuery(id+"F8.opPattern","COPY",BODY,{"derivedFrom":makeQuery(id+"F2.opPattern","COPY",BODY,{"derivedFrom":makeQuery(id+"F1.opRevolve","SWEPT_BODY",BODY,{"disambiguationData":[OSD([sQuery(id+"F0.wireOp",EDGE,"E1")])]}),"instanceName":"1"}),"instanceName":"1"}),"instanceName":"1"}),"instanceName":"1"}),"instanceName":"1"}),"instanceName":"1"});
            var Q2641;
            Q2641=makeQuery(id+"F13.opPattern","COPY",BODY,{"derivedFrom":makeQuery(id+"F12.opPattern","COPY",BODY,{"derivedFrom":makeQuery(id+"F10.opPattern","COPY",BODY,{"derivedFrom":makeQuery(id+"F9.opPattern","COPY",BODY,{"derivedFrom":makeQuery(id+"F8.opPattern","COPY",BODY,{"derivedFrom":makeQuery(id+"F3.opPattern","COPY",BODY,{"derivedFrom":makeQuery(id+"F2.opPattern","COPY",BODY,{"derivedFrom":makeQuery(id+"F1.opRevolve","SWEPT_BODY",BODY,{"disambiguationData":[OSD([sQuery(id+"F0.wireOp",EDGE,"E1")])]}),"instanceName":"1"}),"instanceName":"1"}),"instanceName":"1"}),"instanceName":"1"}),"instanceName":"1"}),"instanceName":"1"}),"instanceName":"1"});
            var Q2642;
            Q2642=makeQuery(id+"F13.opPattern","COPY",BODY,{"derivedFrom":makeQuery(id+"F12.opPattern","COPY",BODY,{"derivedFrom":makeQuery(id+"F10.opPattern","COPY",BODY,{"derivedFrom":makeQuery(id+"F9.opPattern","COPY",BODY,{"derivedFrom":makeQuery(id+"F8.opPattern","COPY",BODY,{"derivedFrom":makeQuery(id+"F4.opPattern","COPY",BODY,{"derivedFrom":makeQuery(id+"F1.opRevolve","SWEPT_BODY",BODY,{"disambiguationData":[OSD([sQuery(id+"F0.wireOp",EDGE,"E1")])]}),"instanceName":"1"}),"instanceName":"1"}),"instanceName":"1"}),"instanceName":"1"}),"instanceName":"1"}),"instanceName":"1"});
            var Q2643;
            Q2643=makeQuery(id+"F13.opPattern","COPY",BODY,{"derivedFrom":makeQuery(id+"F12.opPattern","COPY",BODY,{"derivedFrom":makeQuery(id+"F10.opPattern","COPY",BODY,{"derivedFrom":makeQuery(id+"F9.opPattern","COPY",BODY,{"derivedFrom":makeQuery(id+"F8.opPattern","COPY",BODY,{"derivedFrom":makeQuery(id+"F4.opPattern","COPY",BODY,{"derivedFrom":makeQuery(id+"F2.opPattern","COPY",BODY,{"derivedFrom":makeQuery(id+"F1.opRevolve","SWEPT_BODY",BODY,{"disambiguationData":[OSD([sQuery(id+"F0.wireOp",EDGE,"E1")])]}),"instanceName":"1"}),"instanceName":"1"}),"instanceName":"1"}),"instanceName":"1"}),"instanceName":"1"}),"instanceName":"1"}),"instanceName":"1"});
            var Q2644;
            Q2644=makeQuery(id+"F13.opPattern","COPY",BODY,{"derivedFrom":makeQuery(id+"F12.opPattern","COPY",BODY,{"derivedFrom":makeQuery(id+"F10.opPattern","COPY",BODY,{"derivedFrom":makeQuery(id+"F9.opPattern","COPY",BODY,{"derivedFrom":makeQuery(id+"F8.opPattern","COPY",BODY,{"derivedFrom":makeQuery(id+"F4.opPattern","COPY",BODY,{"derivedFrom":makeQuery(id+"F3.opPattern","COPY",BODY,{"derivedFrom":makeQuery(id+"F2.opPattern","COPY",BODY,{"derivedFrom":makeQuery(id+"F1.opRevolve","SWEPT_BODY",BODY,{"disambiguationData":[OSD([sQuery(id+"F0.wireOp",EDGE,"E1")])]}),"instanceName":"1"}),"instanceName":"1"}),"instanceName":"1"}),"instanceName":"1"}),"instanceName":"1"}),"instanceName":"1"}),"instanceName":"1"}),"instanceName":"1"});
            var Q2645;
            Q2645=makeQuery(id+"F13.opPattern","COPY",BODY,{"derivedFrom":makeQuery(id+"F12.opPattern","COPY",BODY,{"derivedFrom":makeQuery(id+"F10.opPattern","COPY",BODY,{"derivedFrom":makeQuery(id+"F9.opPattern","COPY",BODY,{"derivedFrom":makeQuery(id+"F8.opPattern","COPY",BODY,{"derivedFrom":makeQuery(id+"F5.opPattern","COPY",BODY,{"derivedFrom":makeQuery(id+"F1.opRevolve","SWEPT_BODY",BODY,{"disambiguationData":[OSD([sQuery(id+"F0.wireOp",EDGE,"E1")])]}),"instanceName":"1"}),"instanceName":"1"}),"instanceName":"1"}),"instanceName":"1"}),"instanceName":"1"}),"instanceName":"1"});
            var Q2646;
            Q2646=makeQuery(id+"F13.opPattern","COPY",BODY,{"derivedFrom":makeQuery(id+"F12.opPattern","COPY",BODY,{"derivedFrom":makeQuery(id+"F10.opPattern","COPY",BODY,{"derivedFrom":makeQuery(id+"F9.opPattern","COPY",BODY,{"derivedFrom":makeQuery(id+"F8.opPattern","COPY",BODY,{"derivedFrom":makeQuery(id+"F5.opPattern","COPY",BODY,{"derivedFrom":makeQuery(id+"F2.opPattern","COPY",BODY,{"derivedFrom":makeQuery(id+"F1.opRevolve","SWEPT_BODY",BODY,{"disambiguationData":[OSD([sQuery(id+"F0.wireOp",EDGE,"E1")])]}),"instanceName":"1"}),"instanceName":"1"}),"instanceName":"1"}),"instanceName":"1"}),"instanceName":"1"}),"instanceName":"1"}),"instanceName":"1"});
            var Q2647;
            Q2647=makeQuery(id+"F13.opPattern","COPY",BODY,{"derivedFrom":makeQuery(id+"F12.opPattern","COPY",BODY,{"derivedFrom":makeQuery(id+"F10.opPattern","COPY",BODY,{"derivedFrom":makeQuery(id+"F9.opPattern","COPY",BODY,{"derivedFrom":makeQuery(id+"F8.opPattern","COPY",BODY,{"derivedFrom":makeQuery(id+"F5.opPattern","COPY",BODY,{"derivedFrom":makeQuery(id+"F3.opPattern","COPY",BODY,{"derivedFrom":makeQuery(id+"F2.opPattern","COPY",BODY,{"derivedFrom":makeQuery(id+"F1.opRevolve","SWEPT_BODY",BODY,{"disambiguationData":[OSD([sQuery(id+"F0.wireOp",EDGE,"E1")])]}),"instanceName":"1"}),"instanceName":"1"}),"instanceName":"1"}),"instanceName":"1"}),"instanceName":"1"}),"instanceName":"1"}),"instanceName":"1"}),"instanceName":"1"});
            var Q2648;
            Q2648=makeQuery(id+"F13.opPattern","COPY",BODY,{"derivedFrom":makeQuery(id+"F12.opPattern","COPY",BODY,{"derivedFrom":makeQuery(id+"F10.opPattern","COPY",BODY,{"derivedFrom":makeQuery(id+"F9.opPattern","COPY",BODY,{"derivedFrom":makeQuery(id+"F8.opPattern","COPY",BODY,{"derivedFrom":makeQuery(id+"F5.opPattern","COPY",BODY,{"derivedFrom":makeQuery(id+"F4.opPattern","COPY",BODY,{"derivedFrom":makeQuery(id+"F1.opRevolve","SWEPT_BODY",BODY,{"disambiguationData":[OSD([sQuery(id+"F0.wireOp",EDGE,"E1")])]}),"instanceName":"1"}),"instanceName":"1"}),"instanceName":"1"}),"instanceName":"1"}),"instanceName":"1"}),"instanceName":"1"}),"instanceName":"1"});
            var Q2649;
            Q2649=makeQuery(id+"F13.opPattern","COPY",BODY,{"derivedFrom":makeQuery(id+"F12.opPattern","COPY",BODY,{"derivedFrom":makeQuery(id+"F10.opPattern","COPY",BODY,{"derivedFrom":makeQuery(id+"F9.opPattern","COPY",BODY,{"derivedFrom":makeQuery(id+"F8.opPattern","COPY",BODY,{"derivedFrom":makeQuery(id+"F5.opPattern","COPY",BODY,{"derivedFrom":makeQuery(id+"F4.opPattern","COPY",BODY,{"derivedFrom":makeQuery(id+"F2.opPattern","COPY",BODY,{"derivedFrom":makeQuery(id+"F1.opRevolve","SWEPT_BODY",BODY,{"disambiguationData":[OSD([sQuery(id+"F0.wireOp",EDGE,"E1")])]}),"instanceName":"1"}),"instanceName":"1"}),"instanceName":"1"}),"instanceName":"1"}),"instanceName":"1"}),"instanceName":"1"}),"instanceName":"1"}),"instanceName":"1"});
            var Q2650;
            Q2650=makeQuery(id+"F13.opPattern","COPY",BODY,{"derivedFrom":makeQuery(id+"F12.opPattern","COPY",BODY,{"derivedFrom":makeQuery(id+"F10.opPattern","COPY",BODY,{"derivedFrom":makeQuery(id+"F9.opPattern","COPY",BODY,{"derivedFrom":makeQuery(id+"F8.opPattern","COPY",BODY,{"derivedFrom":makeQuery(id+"F5.opPattern","COPY",BODY,{"derivedFrom":makeQuery(id+"F4.opPattern","COPY",BODY,{"derivedFrom":makeQuery(id+"F3.opPattern","COPY",BODY,{"derivedFrom":makeQuery(id+"F2.opPattern","COPY",BODY,{"derivedFrom":makeQuery(id+"F1.opRevolve","SWEPT_BODY",BODY,{"disambiguationData":[OSD([sQuery(id+"F0.wireOp",EDGE,"E1")])]}),"instanceName":"1"}),"instanceName":"1"}),"instanceName":"1"}),"instanceName":"1"}),"instanceName":"1"}),"instanceName":"1"}),"instanceName":"1"}),"instanceName":"1"}),"instanceName":"1"});
            var Q2651;
            Q2651=makeQuery(id+"F13.opPattern","COPY",BODY,{"derivedFrom":makeQuery(id+"F12.opPattern","COPY",BODY,{"derivedFrom":makeQuery(id+"F10.opPattern","COPY",BODY,{"derivedFrom":makeQuery(id+"F9.opPattern","COPY",BODY,{"derivedFrom":makeQuery(id+"F8.opPattern","COPY",BODY,{"derivedFrom":makeQuery(id+"F6.opPattern","COPY",BODY,{"derivedFrom":makeQuery(id+"F1.opRevolve","SWEPT_BODY",BODY,{"disambiguationData":[OSD([sQuery(id+"F0.wireOp",EDGE,"E1")])]}),"instanceName":"1"}),"instanceName":"1"}),"instanceName":"1"}),"instanceName":"1"}),"instanceName":"1"}),"instanceName":"1"});
            var Q2652;
            Q2652=makeQuery(id+"F13.opPattern","COPY",BODY,{"derivedFrom":makeQuery(id+"F12.opPattern","COPY",BODY,{"derivedFrom":makeQuery(id+"F10.opPattern","COPY",BODY,{"derivedFrom":makeQuery(id+"F9.opPattern","COPY",BODY,{"derivedFrom":makeQuery(id+"F8.opPattern","COPY",BODY,{"derivedFrom":makeQuery(id+"F6.opPattern","COPY",BODY,{"derivedFrom":makeQuery(id+"F2.opPattern","COPY",BODY,{"derivedFrom":makeQuery(id+"F1.opRevolve","SWEPT_BODY",BODY,{"disambiguationData":[OSD([sQuery(id+"F0.wireOp",EDGE,"E1")])]}),"instanceName":"1"}),"instanceName":"1"}),"instanceName":"1"}),"instanceName":"1"}),"instanceName":"1"}),"instanceName":"1"}),"instanceName":"1"});
            var Q2653;
            Q2653=makeQuery(id+"F13.opPattern","COPY",BODY,{"derivedFrom":makeQuery(id+"F12.opPattern","COPY",BODY,{"derivedFrom":makeQuery(id+"F10.opPattern","COPY",BODY,{"derivedFrom":makeQuery(id+"F9.opPattern","COPY",BODY,{"derivedFrom":makeQuery(id+"F8.opPattern","COPY",BODY,{"derivedFrom":makeQuery(id+"F6.opPattern","COPY",BODY,{"derivedFrom":makeQuery(id+"F3.opPattern","COPY",BODY,{"derivedFrom":makeQuery(id+"F2.opPattern","COPY",BODY,{"derivedFrom":makeQuery(id+"F1.opRevolve","SWEPT_BODY",BODY,{"disambiguationData":[OSD([sQuery(id+"F0.wireOp",EDGE,"E1")])]}),"instanceName":"1"}),"instanceName":"1"}),"instanceName":"1"}),"instanceName":"1"}),"instanceName":"1"}),"instanceName":"1"}),"instanceName":"1"}),"instanceName":"1"});
            var Q2654;
            Q2654=makeQuery(id+"F13.opPattern","COPY",BODY,{"derivedFrom":makeQuery(id+"F12.opPattern","COPY",BODY,{"derivedFrom":makeQuery(id+"F10.opPattern","COPY",BODY,{"derivedFrom":makeQuery(id+"F9.opPattern","COPY",BODY,{"derivedFrom":makeQuery(id+"F8.opPattern","COPY",BODY,{"derivedFrom":makeQuery(id+"F6.opPattern","COPY",BODY,{"derivedFrom":makeQuery(id+"F4.opPattern","COPY",BODY,{"derivedFrom":makeQuery(id+"F1.opRevolve","SWEPT_BODY",BODY,{"disambiguationData":[OSD([sQuery(id+"F0.wireOp",EDGE,"E1")])]}),"instanceName":"1"}),"instanceName":"1"}),"instanceName":"1"}),"instanceName":"1"}),"instanceName":"1"}),"instanceName":"1"}),"instanceName":"1"});
            var Q2655;
            Q2655=makeQuery(id+"F13.opPattern","COPY",BODY,{"derivedFrom":makeQuery(id+"F12.opPattern","COPY",BODY,{"derivedFrom":makeQuery(id+"F10.opPattern","COPY",BODY,{"derivedFrom":makeQuery(id+"F9.opPattern","COPY",BODY,{"derivedFrom":makeQuery(id+"F8.opPattern","COPY",BODY,{"derivedFrom":makeQuery(id+"F6.opPattern","COPY",BODY,{"derivedFrom":makeQuery(id+"F4.opPattern","COPY",BODY,{"derivedFrom":makeQuery(id+"F2.opPattern","COPY",BODY,{"derivedFrom":makeQuery(id+"F1.opRevolve","SWEPT_BODY",BODY,{"disambiguationData":[OSD([sQuery(id+"F0.wireOp",EDGE,"E1")])]}),"instanceName":"1"}),"instanceName":"1"}),"instanceName":"1"}),"instanceName":"1"}),"instanceName":"1"}),"instanceName":"1"}),"instanceName":"1"}),"instanceName":"1"});
            var Q2656;
            Q2656=makeQuery(id+"F13.opPattern","COPY",BODY,{"derivedFrom":makeQuery(id+"F12.opPattern","COPY",BODY,{"derivedFrom":makeQuery(id+"F10.opPattern","COPY",BODY,{"derivedFrom":makeQuery(id+"F9.opPattern","COPY",BODY,{"derivedFrom":makeQuery(id+"F8.opPattern","COPY",BODY,{"derivedFrom":makeQuery(id+"F6.opPattern","COPY",BODY,{"derivedFrom":makeQuery(id+"F4.opPattern","COPY",BODY,{"derivedFrom":makeQuery(id+"F3.opPattern","COPY",BODY,{"derivedFrom":makeQuery(id+"F2.opPattern","COPY",BODY,{"derivedFrom":makeQuery(id+"F1.opRevolve","SWEPT_BODY",BODY,{"disambiguationData":[OSD([sQuery(id+"F0.wireOp",EDGE,"E1")])]}),"instanceName":"1"}),"instanceName":"1"}),"instanceName":"1"}),"instanceName":"1"}),"instanceName":"1"}),"instanceName":"1"}),"instanceName":"1"}),"instanceName":"1"}),"instanceName":"1"});
            var Q2657;
            Q2657=makeQuery(id+"F13.opPattern","COPY",BODY,{"derivedFrom":makeQuery(id+"F12.opPattern","COPY",BODY,{"derivedFrom":makeQuery(id+"F10.opPattern","COPY",BODY,{"derivedFrom":makeQuery(id+"F9.opPattern","COPY",BODY,{"derivedFrom":makeQuery(id+"F8.opPattern","COPY",BODY,{"derivedFrom":makeQuery(id+"F6.opPattern","COPY",BODY,{"derivedFrom":makeQuery(id+"F5.opPattern","COPY",BODY,{"derivedFrom":makeQuery(id+"F1.opRevolve","SWEPT_BODY",BODY,{"disambiguationData":[OSD([sQuery(id+"F0.wireOp",EDGE,"E1")])]}),"instanceName":"1"}),"instanceName":"1"}),"instanceName":"1"}),"instanceName":"1"}),"instanceName":"1"}),"instanceName":"1"}),"instanceName":"1"});
            var Q2658;
            Q2658=makeQuery(id+"F13.opPattern","COPY",BODY,{"derivedFrom":makeQuery(id+"F12.opPattern","COPY",BODY,{"derivedFrom":makeQuery(id+"F10.opPattern","COPY",BODY,{"derivedFrom":makeQuery(id+"F9.opPattern","COPY",BODY,{"derivedFrom":makeQuery(id+"F8.opPattern","COPY",BODY,{"derivedFrom":makeQuery(id+"F6.opPattern","COPY",BODY,{"derivedFrom":makeQuery(id+"F5.opPattern","COPY",BODY,{"derivedFrom":makeQuery(id+"F2.opPattern","COPY",BODY,{"derivedFrom":makeQuery(id+"F1.opRevolve","SWEPT_BODY",BODY,{"disambiguationData":[OSD([sQuery(id+"F0.wireOp",EDGE,"E1")])]}),"instanceName":"1"}),"instanceName":"1"}),"instanceName":"1"}),"instanceName":"1"}),"instanceName":"1"}),"instanceName":"1"}),"instanceName":"1"}),"instanceName":"1"});
            var Q2659;
            Q2659=makeQuery(id+"F13.opPattern","COPY",BODY,{"derivedFrom":makeQuery(id+"F12.opPattern","COPY",BODY,{"derivedFrom":makeQuery(id+"F10.opPattern","COPY",BODY,{"derivedFrom":makeQuery(id+"F9.opPattern","COPY",BODY,{"derivedFrom":makeQuery(id+"F8.opPattern","COPY",BODY,{"derivedFrom":makeQuery(id+"F6.opPattern","COPY",BODY,{"derivedFrom":makeQuery(id+"F5.opPattern","COPY",BODY,{"derivedFrom":makeQuery(id+"F3.opPattern","COPY",BODY,{"derivedFrom":makeQuery(id+"F2.opPattern","COPY",BODY,{"derivedFrom":makeQuery(id+"F1.opRevolve","SWEPT_BODY",BODY,{"disambiguationData":[OSD([sQuery(id+"F0.wireOp",EDGE,"E1")])]}),"instanceName":"1"}),"instanceName":"1"}),"instanceName":"1"}),"instanceName":"1"}),"instanceName":"1"}),"instanceName":"1"}),"instanceName":"1"}),"instanceName":"1"}),"instanceName":"1"});
            var Q2660;
            Q2660=makeQuery(id+"F13.opPattern","COPY",BODY,{"derivedFrom":makeQuery(id+"F12.opPattern","COPY",BODY,{"derivedFrom":makeQuery(id+"F10.opPattern","COPY",BODY,{"derivedFrom":makeQuery(id+"F9.opPattern","COPY",BODY,{"derivedFrom":makeQuery(id+"F8.opPattern","COPY",BODY,{"derivedFrom":makeQuery(id+"F6.opPattern","COPY",BODY,{"derivedFrom":makeQuery(id+"F5.opPattern","COPY",BODY,{"derivedFrom":makeQuery(id+"F4.opPattern","COPY",BODY,{"derivedFrom":makeQuery(id+"F1.opRevolve","SWEPT_BODY",BODY,{"disambiguationData":[OSD([sQuery(id+"F0.wireOp",EDGE,"E1")])]}),"instanceName":"1"}),"instanceName":"1"}),"instanceName":"1"}),"instanceName":"1"}),"instanceName":"1"}),"instanceName":"1"}),"instanceName":"1"}),"instanceName":"1"});
            var Q2661;
            Q2661=makeQuery(id+"F13.opPattern","COPY",BODY,{"derivedFrom":makeQuery(id+"F12.opPattern","COPY",BODY,{"derivedFrom":makeQuery(id+"F10.opPattern","COPY",BODY,{"derivedFrom":makeQuery(id+"F9.opPattern","COPY",BODY,{"derivedFrom":makeQuery(id+"F8.opPattern","COPY",BODY,{"derivedFrom":makeQuery(id+"F6.opPattern","COPY",BODY,{"derivedFrom":makeQuery(id+"F5.opPattern","COPY",BODY,{"derivedFrom":makeQuery(id+"F4.opPattern","COPY",BODY,{"derivedFrom":makeQuery(id+"F2.opPattern","COPY",BODY,{"derivedFrom":makeQuery(id+"F1.opRevolve","SWEPT_BODY",BODY,{"disambiguationData":[OSD([sQuery(id+"F0.wireOp",EDGE,"E1")])]}),"instanceName":"1"}),"instanceName":"1"}),"instanceName":"1"}),"instanceName":"1"}),"instanceName":"1"}),"instanceName":"1"}),"instanceName":"1"}),"instanceName":"1"}),"instanceName":"1"});
            var Q2662;
            Q2662=makeQuery(id+"F13.opPattern","COPY",BODY,{"derivedFrom":makeQuery(id+"F12.opPattern","COPY",BODY,{"derivedFrom":makeQuery(id+"F10.opPattern","COPY",BODY,{"derivedFrom":makeQuery(id+"F9.opPattern","COPY",BODY,{"derivedFrom":makeQuery(id+"F8.opPattern","COPY",BODY,{"derivedFrom":makeQuery(id+"F6.opPattern","COPY",BODY,{"derivedFrom":makeQuery(id+"F5.opPattern","COPY",BODY,{"derivedFrom":makeQuery(id+"F4.opPattern","COPY",BODY,{"derivedFrom":makeQuery(id+"F3.opPattern","COPY",BODY,{"derivedFrom":makeQuery(id+"F2.opPattern","COPY",BODY,{"derivedFrom":makeQuery(id+"F1.opRevolve","SWEPT_BODY",BODY,{"disambiguationData":[OSD([sQuery(id+"F0.wireOp",EDGE,"E1")])]}),"instanceName":"1"}),"instanceName":"1"}),"instanceName":"1"}),"instanceName":"1"}),"instanceName":"1"}),"instanceName":"1"}),"instanceName":"1"}),"instanceName":"1"}),"instanceName":"1"}),"instanceName":"1"});
            var Q2663;
            Q2663=makeQuery(id+"F13.opPattern","COPY",BODY,{"derivedFrom":makeQuery(id+"F12.opPattern","COPY",BODY,{"derivedFrom":makeQuery(id+"F10.opPattern","COPY",BODY,{"derivedFrom":makeQuery(id+"F9.opPattern","COPY",BODY,{"derivedFrom":makeQuery(id+"F8.opPattern","COPY",BODY,{"derivedFrom":makeQuery(id+"F7.opPattern","COPY",BODY,{"derivedFrom":makeQuery(id+"F1.opRevolve","SWEPT_BODY",BODY,{"disambiguationData":[OSD([sQuery(id+"F0.wireOp",EDGE,"E1")])]}),"instanceName":"1"}),"instanceName":"1"}),"instanceName":"1"}),"instanceName":"1"}),"instanceName":"1"}),"instanceName":"1"});
            var Q2664;
            Q2664=makeQuery(id+"F13.opPattern","COPY",BODY,{"derivedFrom":makeQuery(id+"F12.opPattern","COPY",BODY,{"derivedFrom":makeQuery(id+"F10.opPattern","COPY",BODY,{"derivedFrom":makeQuery(id+"F9.opPattern","COPY",BODY,{"derivedFrom":makeQuery(id+"F8.opPattern","COPY",BODY,{"derivedFrom":makeQuery(id+"F7.opPattern","COPY",BODY,{"derivedFrom":makeQuery(id+"F2.opPattern","COPY",BODY,{"derivedFrom":makeQuery(id+"F1.opRevolve","SWEPT_BODY",BODY,{"disambiguationData":[OSD([sQuery(id+"F0.wireOp",EDGE,"E1")])]}),"instanceName":"1"}),"instanceName":"1"}),"instanceName":"1"}),"instanceName":"1"}),"instanceName":"1"}),"instanceName":"1"}),"instanceName":"1"});
            var Q2665;
            Q2665=makeQuery(id+"F13.opPattern","COPY",BODY,{"derivedFrom":makeQuery(id+"F12.opPattern","COPY",BODY,{"derivedFrom":makeQuery(id+"F10.opPattern","COPY",BODY,{"derivedFrom":makeQuery(id+"F9.opPattern","COPY",BODY,{"derivedFrom":makeQuery(id+"F8.opPattern","COPY",BODY,{"derivedFrom":makeQuery(id+"F7.opPattern","COPY",BODY,{"derivedFrom":makeQuery(id+"F3.opPattern","COPY",BODY,{"derivedFrom":makeQuery(id+"F2.opPattern","COPY",BODY,{"derivedFrom":makeQuery(id+"F1.opRevolve","SWEPT_BODY",BODY,{"disambiguationData":[OSD([sQuery(id+"F0.wireOp",EDGE,"E1")])]}),"instanceName":"1"}),"instanceName":"1"}),"instanceName":"1"}),"instanceName":"1"}),"instanceName":"1"}),"instanceName":"1"}),"instanceName":"1"}),"instanceName":"1"});
            var Q2666;
            Q2666=makeQuery(id+"F13.opPattern","COPY",BODY,{"derivedFrom":makeQuery(id+"F12.opPattern","COPY",BODY,{"derivedFrom":makeQuery(id+"F10.opPattern","COPY",BODY,{"derivedFrom":makeQuery(id+"F9.opPattern","COPY",BODY,{"derivedFrom":makeQuery(id+"F8.opPattern","COPY",BODY,{"derivedFrom":makeQuery(id+"F7.opPattern","COPY",BODY,{"derivedFrom":makeQuery(id+"F4.opPattern","COPY",BODY,{"derivedFrom":makeQuery(id+"F1.opRevolve","SWEPT_BODY",BODY,{"disambiguationData":[OSD([sQuery(id+"F0.wireOp",EDGE,"E1")])]}),"instanceName":"1"}),"instanceName":"1"}),"instanceName":"1"}),"instanceName":"1"}),"instanceName":"1"}),"instanceName":"1"}),"instanceName":"1"});
            var Q2667;
            Q2667=makeQuery(id+"F13.opPattern","COPY",BODY,{"derivedFrom":makeQuery(id+"F12.opPattern","COPY",BODY,{"derivedFrom":makeQuery(id+"F10.opPattern","COPY",BODY,{"derivedFrom":makeQuery(id+"F9.opPattern","COPY",BODY,{"derivedFrom":makeQuery(id+"F8.opPattern","COPY",BODY,{"derivedFrom":makeQuery(id+"F7.opPattern","COPY",BODY,{"derivedFrom":makeQuery(id+"F4.opPattern","COPY",BODY,{"derivedFrom":makeQuery(id+"F2.opPattern","COPY",BODY,{"derivedFrom":makeQuery(id+"F1.opRevolve","SWEPT_BODY",BODY,{"disambiguationData":[OSD([sQuery(id+"F0.wireOp",EDGE,"E1")])]}),"instanceName":"1"}),"instanceName":"1"}),"instanceName":"1"}),"instanceName":"1"}),"instanceName":"1"}),"instanceName":"1"}),"instanceName":"1"}),"instanceName":"1"});
            var Q2668;
            Q2668=makeQuery(id+"F13.opPattern","COPY",BODY,{"derivedFrom":makeQuery(id+"F12.opPattern","COPY",BODY,{"derivedFrom":makeQuery(id+"F10.opPattern","COPY",BODY,{"derivedFrom":makeQuery(id+"F9.opPattern","COPY",BODY,{"derivedFrom":makeQuery(id+"F8.opPattern","COPY",BODY,{"derivedFrom":makeQuery(id+"F7.opPattern","COPY",BODY,{"derivedFrom":makeQuery(id+"F4.opPattern","COPY",BODY,{"derivedFrom":makeQuery(id+"F3.opPattern","COPY",BODY,{"derivedFrom":makeQuery(id+"F2.opPattern","COPY",BODY,{"derivedFrom":makeQuery(id+"F1.opRevolve","SWEPT_BODY",BODY,{"disambiguationData":[OSD([sQuery(id+"F0.wireOp",EDGE,"E1")])]}),"instanceName":"1"}),"instanceName":"1"}),"instanceName":"1"}),"instanceName":"1"}),"instanceName":"1"}),"instanceName":"1"}),"instanceName":"1"}),"instanceName":"1"}),"instanceName":"1"});
            var Q2669;
            Q2669=makeQuery(id+"F13.opPattern","COPY",BODY,{"derivedFrom":makeQuery(id+"F12.opPattern","COPY",BODY,{"derivedFrom":makeQuery(id+"F10.opPattern","COPY",BODY,{"derivedFrom":makeQuery(id+"F9.opPattern","COPY",BODY,{"derivedFrom":makeQuery(id+"F8.opPattern","COPY",BODY,{"derivedFrom":makeQuery(id+"F7.opPattern","COPY",BODY,{"derivedFrom":makeQuery(id+"F5.opPattern","COPY",BODY,{"derivedFrom":makeQuery(id+"F1.opRevolve","SWEPT_BODY",BODY,{"disambiguationData":[OSD([sQuery(id+"F0.wireOp",EDGE,"E1")])]}),"instanceName":"1"}),"instanceName":"1"}),"instanceName":"1"}),"instanceName":"1"}),"instanceName":"1"}),"instanceName":"1"}),"instanceName":"1"});
            var Q2670;
            Q2670=makeQuery(id+"F13.opPattern","COPY",BODY,{"derivedFrom":makeQuery(id+"F12.opPattern","COPY",BODY,{"derivedFrom":makeQuery(id+"F10.opPattern","COPY",BODY,{"derivedFrom":makeQuery(id+"F9.opPattern","COPY",BODY,{"derivedFrom":makeQuery(id+"F8.opPattern","COPY",BODY,{"derivedFrom":makeQuery(id+"F7.opPattern","COPY",BODY,{"derivedFrom":makeQuery(id+"F5.opPattern","COPY",BODY,{"derivedFrom":makeQuery(id+"F2.opPattern","COPY",BODY,{"derivedFrom":makeQuery(id+"F1.opRevolve","SWEPT_BODY",BODY,{"disambiguationData":[OSD([sQuery(id+"F0.wireOp",EDGE,"E1")])]}),"instanceName":"1"}),"instanceName":"1"}),"instanceName":"1"}),"instanceName":"1"}),"instanceName":"1"}),"instanceName":"1"}),"instanceName":"1"}),"instanceName":"1"});
            var Q2671;
            Q2671=makeQuery(id+"F13.opPattern","COPY",BODY,{"derivedFrom":makeQuery(id+"F12.opPattern","COPY",BODY,{"derivedFrom":makeQuery(id+"F10.opPattern","COPY",BODY,{"derivedFrom":makeQuery(id+"F9.opPattern","COPY",BODY,{"derivedFrom":makeQuery(id+"F8.opPattern","COPY",BODY,{"derivedFrom":makeQuery(id+"F7.opPattern","COPY",BODY,{"derivedFrom":makeQuery(id+"F5.opPattern","COPY",BODY,{"derivedFrom":makeQuery(id+"F3.opPattern","COPY",BODY,{"derivedFrom":makeQuery(id+"F2.opPattern","COPY",BODY,{"derivedFrom":makeQuery(id+"F1.opRevolve","SWEPT_BODY",BODY,{"disambiguationData":[OSD([sQuery(id+"F0.wireOp",EDGE,"E1")])]}),"instanceName":"1"}),"instanceName":"1"}),"instanceName":"1"}),"instanceName":"1"}),"instanceName":"1"}),"instanceName":"1"}),"instanceName":"1"}),"instanceName":"1"}),"instanceName":"1"});
            var Q2672;
            Q2672=makeQuery(id+"F13.opPattern","COPY",BODY,{"derivedFrom":makeQuery(id+"F12.opPattern","COPY",BODY,{"derivedFrom":makeQuery(id+"F10.opPattern","COPY",BODY,{"derivedFrom":makeQuery(id+"F9.opPattern","COPY",BODY,{"derivedFrom":makeQuery(id+"F8.opPattern","COPY",BODY,{"derivedFrom":makeQuery(id+"F7.opPattern","COPY",BODY,{"derivedFrom":makeQuery(id+"F5.opPattern","COPY",BODY,{"derivedFrom":makeQuery(id+"F4.opPattern","COPY",BODY,{"derivedFrom":makeQuery(id+"F1.opRevolve","SWEPT_BODY",BODY,{"disambiguationData":[OSD([sQuery(id+"F0.wireOp",EDGE,"E1")])]}),"instanceName":"1"}),"instanceName":"1"}),"instanceName":"1"}),"instanceName":"1"}),"instanceName":"1"}),"instanceName":"1"}),"instanceName":"1"}),"instanceName":"1"});
            var Q2673;
            Q2673=makeQuery(id+"F13.opPattern","COPY",BODY,{"derivedFrom":makeQuery(id+"F12.opPattern","COPY",BODY,{"derivedFrom":makeQuery(id+"F10.opPattern","COPY",BODY,{"derivedFrom":makeQuery(id+"F9.opPattern","COPY",BODY,{"derivedFrom":makeQuery(id+"F8.opPattern","COPY",BODY,{"derivedFrom":makeQuery(id+"F7.opPattern","COPY",BODY,{"derivedFrom":makeQuery(id+"F5.opPattern","COPY",BODY,{"derivedFrom":makeQuery(id+"F4.opPattern","COPY",BODY,{"derivedFrom":makeQuery(id+"F2.opPattern","COPY",BODY,{"derivedFrom":makeQuery(id+"F1.opRevolve","SWEPT_BODY",BODY,{"disambiguationData":[OSD([sQuery(id+"F0.wireOp",EDGE,"E1")])]}),"instanceName":"1"}),"instanceName":"1"}),"instanceName":"1"}),"instanceName":"1"}),"instanceName":"1"}),"instanceName":"1"}),"instanceName":"1"}),"instanceName":"1"}),"instanceName":"1"});
            var Q2674;
            Q2674=makeQuery(id+"F13.opPattern","COPY",BODY,{"derivedFrom":makeQuery(id+"F12.opPattern","COPY",BODY,{"derivedFrom":makeQuery(id+"F10.opPattern","COPY",BODY,{"derivedFrom":makeQuery(id+"F9.opPattern","COPY",BODY,{"derivedFrom":makeQuery(id+"F8.opPattern","COPY",BODY,{"derivedFrom":makeQuery(id+"F7.opPattern","COPY",BODY,{"derivedFrom":makeQuery(id+"F5.opPattern","COPY",BODY,{"derivedFrom":makeQuery(id+"F4.opPattern","COPY",BODY,{"derivedFrom":makeQuery(id+"F3.opPattern","COPY",BODY,{"derivedFrom":makeQuery(id+"F2.opPattern","COPY",BODY,{"derivedFrom":makeQuery(id+"F1.opRevolve","SWEPT_BODY",BODY,{"disambiguationData":[OSD([sQuery(id+"F0.wireOp",EDGE,"E1")])]}),"instanceName":"1"}),"instanceName":"1"}),"instanceName":"1"}),"instanceName":"1"}),"instanceName":"1"}),"instanceName":"1"}),"instanceName":"1"}),"instanceName":"1"}),"instanceName":"1"}),"instanceName":"1"});
            var Q2675;
            Q2675=makeQuery(id+"F13.opPattern","COPY",BODY,{"derivedFrom":makeQuery(id+"F12.opPattern","COPY",BODY,{"derivedFrom":makeQuery(id+"F10.opPattern","COPY",BODY,{"derivedFrom":makeQuery(id+"F9.opPattern","COPY",BODY,{"derivedFrom":makeQuery(id+"F8.opPattern","COPY",BODY,{"derivedFrom":makeQuery(id+"F7.opPattern","COPY",BODY,{"derivedFrom":makeQuery(id+"F6.opPattern","COPY",BODY,{"derivedFrom":makeQuery(id+"F1.opRevolve","SWEPT_BODY",BODY,{"disambiguationData":[OSD([sQuery(id+"F0.wireOp",EDGE,"E1")])]}),"instanceName":"1"}),"instanceName":"1"}),"instanceName":"1"}),"instanceName":"1"}),"instanceName":"1"}),"instanceName":"1"}),"instanceName":"1"});
            var Q2676;
            Q2676=makeQuery(id+"F13.opPattern","COPY",BODY,{"derivedFrom":makeQuery(id+"F12.opPattern","COPY",BODY,{"derivedFrom":makeQuery(id+"F10.opPattern","COPY",BODY,{"derivedFrom":makeQuery(id+"F9.opPattern","COPY",BODY,{"derivedFrom":makeQuery(id+"F8.opPattern","COPY",BODY,{"derivedFrom":makeQuery(id+"F7.opPattern","COPY",BODY,{"derivedFrom":makeQuery(id+"F6.opPattern","COPY",BODY,{"derivedFrom":makeQuery(id+"F2.opPattern","COPY",BODY,{"derivedFrom":makeQuery(id+"F1.opRevolve","SWEPT_BODY",BODY,{"disambiguationData":[OSD([sQuery(id+"F0.wireOp",EDGE,"E1")])]}),"instanceName":"1"}),"instanceName":"1"}),"instanceName":"1"}),"instanceName":"1"}),"instanceName":"1"}),"instanceName":"1"}),"instanceName":"1"}),"instanceName":"1"});
            var Q2677;
            Q2677=makeQuery(id+"F13.opPattern","COPY",BODY,{"derivedFrom":makeQuery(id+"F12.opPattern","COPY",BODY,{"derivedFrom":makeQuery(id+"F10.opPattern","COPY",BODY,{"derivedFrom":makeQuery(id+"F9.opPattern","COPY",BODY,{"derivedFrom":makeQuery(id+"F8.opPattern","COPY",BODY,{"derivedFrom":makeQuery(id+"F7.opPattern","COPY",BODY,{"derivedFrom":makeQuery(id+"F6.opPattern","COPY",BODY,{"derivedFrom":makeQuery(id+"F3.opPattern","COPY",BODY,{"derivedFrom":makeQuery(id+"F2.opPattern","COPY",BODY,{"derivedFrom":makeQuery(id+"F1.opRevolve","SWEPT_BODY",BODY,{"disambiguationData":[OSD([sQuery(id+"F0.wireOp",EDGE,"E1")])]}),"instanceName":"1"}),"instanceName":"1"}),"instanceName":"1"}),"instanceName":"1"}),"instanceName":"1"}),"instanceName":"1"}),"instanceName":"1"}),"instanceName":"1"}),"instanceName":"1"});
            var Q2678;
            Q2678=makeQuery(id+"F13.opPattern","COPY",BODY,{"derivedFrom":makeQuery(id+"F12.opPattern","COPY",BODY,{"derivedFrom":makeQuery(id+"F10.opPattern","COPY",BODY,{"derivedFrom":makeQuery(id+"F9.opPattern","COPY",BODY,{"derivedFrom":makeQuery(id+"F8.opPattern","COPY",BODY,{"derivedFrom":makeQuery(id+"F7.opPattern","COPY",BODY,{"derivedFrom":makeQuery(id+"F6.opPattern","COPY",BODY,{"derivedFrom":makeQuery(id+"F4.opPattern","COPY",BODY,{"derivedFrom":makeQuery(id+"F1.opRevolve","SWEPT_BODY",BODY,{"disambiguationData":[OSD([sQuery(id+"F0.wireOp",EDGE,"E1")])]}),"instanceName":"1"}),"instanceName":"1"}),"instanceName":"1"}),"instanceName":"1"}),"instanceName":"1"}),"instanceName":"1"}),"instanceName":"1"}),"instanceName":"1"});
            var Q2679;
            Q2679=makeQuery(id+"F13.opPattern","COPY",BODY,{"derivedFrom":makeQuery(id+"F12.opPattern","COPY",BODY,{"derivedFrom":makeQuery(id+"F10.opPattern","COPY",BODY,{"derivedFrom":makeQuery(id+"F9.opPattern","COPY",BODY,{"derivedFrom":makeQuery(id+"F8.opPattern","COPY",BODY,{"derivedFrom":makeQuery(id+"F7.opPattern","COPY",BODY,{"derivedFrom":makeQuery(id+"F6.opPattern","COPY",BODY,{"derivedFrom":makeQuery(id+"F4.opPattern","COPY",BODY,{"derivedFrom":makeQuery(id+"F2.opPattern","COPY",BODY,{"derivedFrom":makeQuery(id+"F1.opRevolve","SWEPT_BODY",BODY,{"disambiguationData":[OSD([sQuery(id+"F0.wireOp",EDGE,"E1")])]}),"instanceName":"1"}),"instanceName":"1"}),"instanceName":"1"}),"instanceName":"1"}),"instanceName":"1"}),"instanceName":"1"}),"instanceName":"1"}),"instanceName":"1"}),"instanceName":"1"});
            var Q2680;
            Q2680=makeQuery(id+"F13.opPattern","COPY",BODY,{"derivedFrom":makeQuery(id+"F12.opPattern","COPY",BODY,{"derivedFrom":makeQuery(id+"F10.opPattern","COPY",BODY,{"derivedFrom":makeQuery(id+"F9.opPattern","COPY",BODY,{"derivedFrom":makeQuery(id+"F8.opPattern","COPY",BODY,{"derivedFrom":makeQuery(id+"F7.opPattern","COPY",BODY,{"derivedFrom":makeQuery(id+"F6.opPattern","COPY",BODY,{"derivedFrom":makeQuery(id+"F4.opPattern","COPY",BODY,{"derivedFrom":makeQuery(id+"F3.opPattern","COPY",BODY,{"derivedFrom":makeQuery(id+"F2.opPattern","COPY",BODY,{"derivedFrom":makeQuery(id+"F1.opRevolve","SWEPT_BODY",BODY,{"disambiguationData":[OSD([sQuery(id+"F0.wireOp",EDGE,"E1")])]}),"instanceName":"1"}),"instanceName":"1"}),"instanceName":"1"}),"instanceName":"1"}),"instanceName":"1"}),"instanceName":"1"}),"instanceName":"1"}),"instanceName":"1"}),"instanceName":"1"}),"instanceName":"1"});
            var Q2681;
            Q2681=makeQuery(id+"F13.opPattern","COPY",BODY,{"derivedFrom":makeQuery(id+"F12.opPattern","COPY",BODY,{"derivedFrom":makeQuery(id+"F10.opPattern","COPY",BODY,{"derivedFrom":makeQuery(id+"F9.opPattern","COPY",BODY,{"derivedFrom":makeQuery(id+"F8.opPattern","COPY",BODY,{"derivedFrom":makeQuery(id+"F7.opPattern","COPY",BODY,{"derivedFrom":makeQuery(id+"F6.opPattern","COPY",BODY,{"derivedFrom":makeQuery(id+"F5.opPattern","COPY",BODY,{"derivedFrom":makeQuery(id+"F1.opRevolve","SWEPT_BODY",BODY,{"disambiguationData":[OSD([sQuery(id+"F0.wireOp",EDGE,"E1")])]}),"instanceName":"1"}),"instanceName":"1"}),"instanceName":"1"}),"instanceName":"1"}),"instanceName":"1"}),"instanceName":"1"}),"instanceName":"1"}),"instanceName":"1"});
            var Q2682;
            Q2682=makeQuery(id+"F13.opPattern","COPY",BODY,{"derivedFrom":makeQuery(id+"F12.opPattern","COPY",BODY,{"derivedFrom":makeQuery(id+"F10.opPattern","COPY",BODY,{"derivedFrom":makeQuery(id+"F9.opPattern","COPY",BODY,{"derivedFrom":makeQuery(id+"F8.opPattern","COPY",BODY,{"derivedFrom":makeQuery(id+"F7.opPattern","COPY",BODY,{"derivedFrom":makeQuery(id+"F6.opPattern","COPY",BODY,{"derivedFrom":makeQuery(id+"F5.opPattern","COPY",BODY,{"derivedFrom":makeQuery(id+"F2.opPattern","COPY",BODY,{"derivedFrom":makeQuery(id+"F1.opRevolve","SWEPT_BODY",BODY,{"disambiguationData":[OSD([sQuery(id+"F0.wireOp",EDGE,"E1")])]}),"instanceName":"1"}),"instanceName":"1"}),"instanceName":"1"}),"instanceName":"1"}),"instanceName":"1"}),"instanceName":"1"}),"instanceName":"1"}),"instanceName":"1"}),"instanceName":"1"});
            var Q2683;
            Q2683=makeQuery(id+"F13.opPattern","COPY",BODY,{"derivedFrom":makeQuery(id+"F12.opPattern","COPY",BODY,{"derivedFrom":makeQuery(id+"F10.opPattern","COPY",BODY,{"derivedFrom":makeQuery(id+"F9.opPattern","COPY",BODY,{"derivedFrom":makeQuery(id+"F8.opPattern","COPY",BODY,{"derivedFrom":makeQuery(id+"F7.opPattern","COPY",BODY,{"derivedFrom":makeQuery(id+"F6.opPattern","COPY",BODY,{"derivedFrom":makeQuery(id+"F5.opPattern","COPY",BODY,{"derivedFrom":makeQuery(id+"F3.opPattern","COPY",BODY,{"derivedFrom":makeQuery(id+"F2.opPattern","COPY",BODY,{"derivedFrom":makeQuery(id+"F1.opRevolve","SWEPT_BODY",BODY,{"disambiguationData":[OSD([sQuery(id+"F0.wireOp",EDGE,"E1")])]}),"instanceName":"1"}),"instanceName":"1"}),"instanceName":"1"}),"instanceName":"1"}),"instanceName":"1"}),"instanceName":"1"}),"instanceName":"1"}),"instanceName":"1"}),"instanceName":"1"}),"instanceName":"1"});
            var Q2684;
            Q2684=makeQuery(id+"F13.opPattern","COPY",BODY,{"derivedFrom":makeQuery(id+"F12.opPattern","COPY",BODY,{"derivedFrom":makeQuery(id+"F10.opPattern","COPY",BODY,{"derivedFrom":makeQuery(id+"F9.opPattern","COPY",BODY,{"derivedFrom":makeQuery(id+"F8.opPattern","COPY",BODY,{"derivedFrom":makeQuery(id+"F7.opPattern","COPY",BODY,{"derivedFrom":makeQuery(id+"F6.opPattern","COPY",BODY,{"derivedFrom":makeQuery(id+"F5.opPattern","COPY",BODY,{"derivedFrom":makeQuery(id+"F4.opPattern","COPY",BODY,{"derivedFrom":makeQuery(id+"F1.opRevolve","SWEPT_BODY",BODY,{"disambiguationData":[OSD([sQuery(id+"F0.wireOp",EDGE,"E1")])]}),"instanceName":"1"}),"instanceName":"1"}),"instanceName":"1"}),"instanceName":"1"}),"instanceName":"1"}),"instanceName":"1"}),"instanceName":"1"}),"instanceName":"1"}),"instanceName":"1"});
            var Q2685;
            Q2685=makeQuery(id+"F13.opPattern","COPY",BODY,{"derivedFrom":makeQuery(id+"F12.opPattern","COPY",BODY,{"derivedFrom":makeQuery(id+"F10.opPattern","COPY",BODY,{"derivedFrom":makeQuery(id+"F9.opPattern","COPY",BODY,{"derivedFrom":makeQuery(id+"F8.opPattern","COPY",BODY,{"derivedFrom":makeQuery(id+"F7.opPattern","COPY",BODY,{"derivedFrom":makeQuery(id+"F6.opPattern","COPY",BODY,{"derivedFrom":makeQuery(id+"F5.opPattern","COPY",BODY,{"derivedFrom":makeQuery(id+"F4.opPattern","COPY",BODY,{"derivedFrom":makeQuery(id+"F2.opPattern","COPY",BODY,{"derivedFrom":makeQuery(id+"F1.opRevolve","SWEPT_BODY",BODY,{"disambiguationData":[OSD([sQuery(id+"F0.wireOp",EDGE,"E1")])]}),"instanceName":"1"}),"instanceName":"1"}),"instanceName":"1"}),"instanceName":"1"}),"instanceName":"1"}),"instanceName":"1"}),"instanceName":"1"}),"instanceName":"1"}),"instanceName":"1"}),"instanceName":"1"});
            var Q2686;
            Q2686=makeQuery(id+"F13.opPattern","COPY",BODY,{"derivedFrom":makeQuery(id+"F12.opPattern","COPY",BODY,{"derivedFrom":makeQuery(id+"F10.opPattern","COPY",BODY,{"derivedFrom":makeQuery(id+"F9.opPattern","COPY",BODY,{"derivedFrom":makeQuery(id+"F8.opPattern","COPY",BODY,{"derivedFrom":makeQuery(id+"F7.opPattern","COPY",BODY,{"derivedFrom":makeQuery(id+"F6.opPattern","COPY",BODY,{"derivedFrom":makeQuery(id+"F5.opPattern","COPY",BODY,{"derivedFrom":makeQuery(id+"F4.opPattern","COPY",BODY,{"derivedFrom":makeQuery(id+"F3.opPattern","COPY",BODY,{"derivedFrom":makeQuery(id+"F2.opPattern","COPY",BODY,{"derivedFrom":makeQuery(id+"F1.opRevolve","SWEPT_BODY",BODY,{"disambiguationData":[OSD([sQuery(id+"F0.wireOp",EDGE,"E1")])]}),"instanceName":"1"}),"instanceName":"1"}),"instanceName":"1"}),"instanceName":"1"}),"instanceName":"1"}),"instanceName":"1"}),"instanceName":"1"}),"instanceName":"1"}),"instanceName":"1"}),"instanceName":"1"}),"instanceName":"1"});
            var Q2687;
            Q2687=makeQuery(id+"F13.opPattern","COPY",BODY,{"derivedFrom":makeQuery(id+"F12.opPattern","COPY",BODY,{"derivedFrom":makeQuery(id+"F11.opPattern","COPY",BODY,{"derivedFrom":makeQuery(id+"F1.opRevolve","SWEPT_BODY",BODY,{"disambiguationData":[OSD([sQuery(id+"F0.wireOp",EDGE,"E1")])]}),"instanceName":"1"}),"instanceName":"1"}),"instanceName":"1"});
            var Q2688;
            Q2688=makeQuery(id+"F13.opPattern","COPY",BODY,{"derivedFrom":makeQuery(id+"F12.opPattern","COPY",BODY,{"derivedFrom":makeQuery(id+"F11.opPattern","COPY",BODY,{"derivedFrom":makeQuery(id+"F2.opPattern","COPY",BODY,{"derivedFrom":makeQuery(id+"F1.opRevolve","SWEPT_BODY",BODY,{"disambiguationData":[OSD([sQuery(id+"F0.wireOp",EDGE,"E1")])]}),"instanceName":"1"}),"instanceName":"1"}),"instanceName":"1"}),"instanceName":"1"});
            var Q2689;
            Q2689=makeQuery(id+"F13.opPattern","COPY",BODY,{"derivedFrom":makeQuery(id+"F12.opPattern","COPY",BODY,{"derivedFrom":makeQuery(id+"F11.opPattern","COPY",BODY,{"derivedFrom":makeQuery(id+"F3.opPattern","COPY",BODY,{"derivedFrom":makeQuery(id+"F2.opPattern","COPY",BODY,{"derivedFrom":makeQuery(id+"F1.opRevolve","SWEPT_BODY",BODY,{"disambiguationData":[OSD([sQuery(id+"F0.wireOp",EDGE,"E1")])]}),"instanceName":"1"}),"instanceName":"1"}),"instanceName":"1"}),"instanceName":"1"}),"instanceName":"1"});
            var Q2690;
            Q2690=makeQuery(id+"F13.opPattern","COPY",BODY,{"derivedFrom":makeQuery(id+"F12.opPattern","COPY",BODY,{"derivedFrom":makeQuery(id+"F11.opPattern","COPY",BODY,{"derivedFrom":makeQuery(id+"F4.opPattern","COPY",BODY,{"derivedFrom":makeQuery(id+"F1.opRevolve","SWEPT_BODY",BODY,{"disambiguationData":[OSD([sQuery(id+"F0.wireOp",EDGE,"E1")])]}),"instanceName":"1"}),"instanceName":"1"}),"instanceName":"1"}),"instanceName":"1"});
            var Q2691;
            Q2691=makeQuery(id+"F13.opPattern","COPY",BODY,{"derivedFrom":makeQuery(id+"F12.opPattern","COPY",BODY,{"derivedFrom":makeQuery(id+"F11.opPattern","COPY",BODY,{"derivedFrom":makeQuery(id+"F4.opPattern","COPY",BODY,{"derivedFrom":makeQuery(id+"F2.opPattern","COPY",BODY,{"derivedFrom":makeQuery(id+"F1.opRevolve","SWEPT_BODY",BODY,{"disambiguationData":[OSD([sQuery(id+"F0.wireOp",EDGE,"E1")])]}),"instanceName":"1"}),"instanceName":"1"}),"instanceName":"1"}),"instanceName":"1"}),"instanceName":"1"});
            var Q2692;
            Q2692=makeQuery(id+"F13.opPattern","COPY",BODY,{"derivedFrom":makeQuery(id+"F12.opPattern","COPY",BODY,{"derivedFrom":makeQuery(id+"F11.opPattern","COPY",BODY,{"derivedFrom":makeQuery(id+"F4.opPattern","COPY",BODY,{"derivedFrom":makeQuery(id+"F3.opPattern","COPY",BODY,{"derivedFrom":makeQuery(id+"F2.opPattern","COPY",BODY,{"derivedFrom":makeQuery(id+"F1.opRevolve","SWEPT_BODY",BODY,{"disambiguationData":[OSD([sQuery(id+"F0.wireOp",EDGE,"E1")])]}),"instanceName":"1"}),"instanceName":"1"}),"instanceName":"1"}),"instanceName":"1"}),"instanceName":"1"}),"instanceName":"1"});
            var Q2693;
            Q2693=makeQuery(id+"F13.opPattern","COPY",BODY,{"derivedFrom":makeQuery(id+"F12.opPattern","COPY",BODY,{"derivedFrom":makeQuery(id+"F11.opPattern","COPY",BODY,{"derivedFrom":makeQuery(id+"F5.opPattern","COPY",BODY,{"derivedFrom":makeQuery(id+"F1.opRevolve","SWEPT_BODY",BODY,{"disambiguationData":[OSD([sQuery(id+"F0.wireOp",EDGE,"E1")])]}),"instanceName":"1"}),"instanceName":"1"}),"instanceName":"1"}),"instanceName":"1"});
            var Q2694;
            Q2694=makeQuery(id+"F13.opPattern","COPY",BODY,{"derivedFrom":makeQuery(id+"F12.opPattern","COPY",BODY,{"derivedFrom":makeQuery(id+"F11.opPattern","COPY",BODY,{"derivedFrom":makeQuery(id+"F5.opPattern","COPY",BODY,{"derivedFrom":makeQuery(id+"F2.opPattern","COPY",BODY,{"derivedFrom":makeQuery(id+"F1.opRevolve","SWEPT_BODY",BODY,{"disambiguationData":[OSD([sQuery(id+"F0.wireOp",EDGE,"E1")])]}),"instanceName":"1"}),"instanceName":"1"}),"instanceName":"1"}),"instanceName":"1"}),"instanceName":"1"});
            var Q2695;
            Q2695=makeQuery(id+"F13.opPattern","COPY",BODY,{"derivedFrom":makeQuery(id+"F12.opPattern","COPY",BODY,{"derivedFrom":makeQuery(id+"F11.opPattern","COPY",BODY,{"derivedFrom":makeQuery(id+"F5.opPattern","COPY",BODY,{"derivedFrom":makeQuery(id+"F3.opPattern","COPY",BODY,{"derivedFrom":makeQuery(id+"F2.opPattern","COPY",BODY,{"derivedFrom":makeQuery(id+"F1.opRevolve","SWEPT_BODY",BODY,{"disambiguationData":[OSD([sQuery(id+"F0.wireOp",EDGE,"E1")])]}),"instanceName":"1"}),"instanceName":"1"}),"instanceName":"1"}),"instanceName":"1"}),"instanceName":"1"}),"instanceName":"1"});
            var Q2696;
            Q2696=makeQuery(id+"F13.opPattern","COPY",BODY,{"derivedFrom":makeQuery(id+"F12.opPattern","COPY",BODY,{"derivedFrom":makeQuery(id+"F11.opPattern","COPY",BODY,{"derivedFrom":makeQuery(id+"F5.opPattern","COPY",BODY,{"derivedFrom":makeQuery(id+"F4.opPattern","COPY",BODY,{"derivedFrom":makeQuery(id+"F1.opRevolve","SWEPT_BODY",BODY,{"disambiguationData":[OSD([sQuery(id+"F0.wireOp",EDGE,"E1")])]}),"instanceName":"1"}),"instanceName":"1"}),"instanceName":"1"}),"instanceName":"1"}),"instanceName":"1"});
            var Q2697;
            Q2697=makeQuery(id+"F13.opPattern","COPY",BODY,{"derivedFrom":makeQuery(id+"F12.opPattern","COPY",BODY,{"derivedFrom":makeQuery(id+"F11.opPattern","COPY",BODY,{"derivedFrom":makeQuery(id+"F5.opPattern","COPY",BODY,{"derivedFrom":makeQuery(id+"F4.opPattern","COPY",BODY,{"derivedFrom":makeQuery(id+"F2.opPattern","COPY",BODY,{"derivedFrom":makeQuery(id+"F1.opRevolve","SWEPT_BODY",BODY,{"disambiguationData":[OSD([sQuery(id+"F0.wireOp",EDGE,"E1")])]}),"instanceName":"1"}),"instanceName":"1"}),"instanceName":"1"}),"instanceName":"1"}),"instanceName":"1"}),"instanceName":"1"});
            var Q2698;
            Q2698=makeQuery(id+"F13.opPattern","COPY",BODY,{"derivedFrom":makeQuery(id+"F12.opPattern","COPY",BODY,{"derivedFrom":makeQuery(id+"F11.opPattern","COPY",BODY,{"derivedFrom":makeQuery(id+"F5.opPattern","COPY",BODY,{"derivedFrom":makeQuery(id+"F4.opPattern","COPY",BODY,{"derivedFrom":makeQuery(id+"F3.opPattern","COPY",BODY,{"derivedFrom":makeQuery(id+"F2.opPattern","COPY",BODY,{"derivedFrom":makeQuery(id+"F1.opRevolve","SWEPT_BODY",BODY,{"disambiguationData":[OSD([sQuery(id+"F0.wireOp",EDGE,"E1")])]}),"instanceName":"1"}),"instanceName":"1"}),"instanceName":"1"}),"instanceName":"1"}),"instanceName":"1"}),"instanceName":"1"}),"instanceName":"1"});
            var Q2699;
            Q2699=makeQuery(id+"F13.opPattern","COPY",BODY,{"derivedFrom":makeQuery(id+"F12.opPattern","COPY",BODY,{"derivedFrom":makeQuery(id+"F11.opPattern","COPY",BODY,{"derivedFrom":makeQuery(id+"F6.opPattern","COPY",BODY,{"derivedFrom":makeQuery(id+"F1.opRevolve","SWEPT_BODY",BODY,{"disambiguationData":[OSD([sQuery(id+"F0.wireOp",EDGE,"E1")])]}),"instanceName":"1"}),"instanceName":"1"}),"instanceName":"1"}),"instanceName":"1"});
            var Q2700;
            Q2700=makeQuery(id+"F13.opPattern","COPY",BODY,{"derivedFrom":makeQuery(id+"F12.opPattern","COPY",BODY,{"derivedFrom":makeQuery(id+"F11.opPattern","COPY",BODY,{"derivedFrom":makeQuery(id+"F6.opPattern","COPY",BODY,{"derivedFrom":makeQuery(id+"F2.opPattern","COPY",BODY,{"derivedFrom":makeQuery(id+"F1.opRevolve","SWEPT_BODY",BODY,{"disambiguationData":[OSD([sQuery(id+"F0.wireOp",EDGE,"E1")])]}),"instanceName":"1"}),"instanceName":"1"}),"instanceName":"1"}),"instanceName":"1"}),"instanceName":"1"});
            var Q2701;
            Q2701=makeQuery(id+"F13.opPattern","COPY",BODY,{"derivedFrom":makeQuery(id+"F12.opPattern","COPY",BODY,{"derivedFrom":makeQuery(id+"F11.opPattern","COPY",BODY,{"derivedFrom":makeQuery(id+"F6.opPattern","COPY",BODY,{"derivedFrom":makeQuery(id+"F3.opPattern","COPY",BODY,{"derivedFrom":makeQuery(id+"F2.opPattern","COPY",BODY,{"derivedFrom":makeQuery(id+"F1.opRevolve","SWEPT_BODY",BODY,{"disambiguationData":[OSD([sQuery(id+"F0.wireOp",EDGE,"E1")])]}),"instanceName":"1"}),"instanceName":"1"}),"instanceName":"1"}),"instanceName":"1"}),"instanceName":"1"}),"instanceName":"1"});
            var Q2702;
            Q2702=makeQuery(id+"F13.opPattern","COPY",BODY,{"derivedFrom":makeQuery(id+"F12.opPattern","COPY",BODY,{"derivedFrom":makeQuery(id+"F11.opPattern","COPY",BODY,{"derivedFrom":makeQuery(id+"F6.opPattern","COPY",BODY,{"derivedFrom":makeQuery(id+"F4.opPattern","COPY",BODY,{"derivedFrom":makeQuery(id+"F1.opRevolve","SWEPT_BODY",BODY,{"disambiguationData":[OSD([sQuery(id+"F0.wireOp",EDGE,"E1")])]}),"instanceName":"1"}),"instanceName":"1"}),"instanceName":"1"}),"instanceName":"1"}),"instanceName":"1"});
            var Q2703;
            Q2703=makeQuery(id+"F13.opPattern","COPY",BODY,{"derivedFrom":makeQuery(id+"F12.opPattern","COPY",BODY,{"derivedFrom":makeQuery(id+"F11.opPattern","COPY",BODY,{"derivedFrom":makeQuery(id+"F6.opPattern","COPY",BODY,{"derivedFrom":makeQuery(id+"F4.opPattern","COPY",BODY,{"derivedFrom":makeQuery(id+"F2.opPattern","COPY",BODY,{"derivedFrom":makeQuery(id+"F1.opRevolve","SWEPT_BODY",BODY,{"disambiguationData":[OSD([sQuery(id+"F0.wireOp",EDGE,"E1")])]}),"instanceName":"1"}),"instanceName":"1"}),"instanceName":"1"}),"instanceName":"1"}),"instanceName":"1"}),"instanceName":"1"});
            var Q2704;
            Q2704=makeQuery(id+"F13.opPattern","COPY",BODY,{"derivedFrom":makeQuery(id+"F12.opPattern","COPY",BODY,{"derivedFrom":makeQuery(id+"F11.opPattern","COPY",BODY,{"derivedFrom":makeQuery(id+"F6.opPattern","COPY",BODY,{"derivedFrom":makeQuery(id+"F4.opPattern","COPY",BODY,{"derivedFrom":makeQuery(id+"F3.opPattern","COPY",BODY,{"derivedFrom":makeQuery(id+"F2.opPattern","COPY",BODY,{"derivedFrom":makeQuery(id+"F1.opRevolve","SWEPT_BODY",BODY,{"disambiguationData":[OSD([sQuery(id+"F0.wireOp",EDGE,"E1")])]}),"instanceName":"1"}),"instanceName":"1"}),"instanceName":"1"}),"instanceName":"1"}),"instanceName":"1"}),"instanceName":"1"}),"instanceName":"1"});
            var Q2705;
            Q2705=makeQuery(id+"F13.opPattern","COPY",BODY,{"derivedFrom":makeQuery(id+"F12.opPattern","COPY",BODY,{"derivedFrom":makeQuery(id+"F11.opPattern","COPY",BODY,{"derivedFrom":makeQuery(id+"F6.opPattern","COPY",BODY,{"derivedFrom":makeQuery(id+"F5.opPattern","COPY",BODY,{"derivedFrom":makeQuery(id+"F1.opRevolve","SWEPT_BODY",BODY,{"disambiguationData":[OSD([sQuery(id+"F0.wireOp",EDGE,"E1")])]}),"instanceName":"1"}),"instanceName":"1"}),"instanceName":"1"}),"instanceName":"1"}),"instanceName":"1"});
            var Q2706;
            Q2706=makeQuery(id+"F13.opPattern","COPY",BODY,{"derivedFrom":makeQuery(id+"F12.opPattern","COPY",BODY,{"derivedFrom":makeQuery(id+"F11.opPattern","COPY",BODY,{"derivedFrom":makeQuery(id+"F6.opPattern","COPY",BODY,{"derivedFrom":makeQuery(id+"F5.opPattern","COPY",BODY,{"derivedFrom":makeQuery(id+"F2.opPattern","COPY",BODY,{"derivedFrom":makeQuery(id+"F1.opRevolve","SWEPT_BODY",BODY,{"disambiguationData":[OSD([sQuery(id+"F0.wireOp",EDGE,"E1")])]}),"instanceName":"1"}),"instanceName":"1"}),"instanceName":"1"}),"instanceName":"1"}),"instanceName":"1"}),"instanceName":"1"});
            var Q2707;
            Q2707=makeQuery(id+"F13.opPattern","COPY",BODY,{"derivedFrom":makeQuery(id+"F12.opPattern","COPY",BODY,{"derivedFrom":makeQuery(id+"F11.opPattern","COPY",BODY,{"derivedFrom":makeQuery(id+"F6.opPattern","COPY",BODY,{"derivedFrom":makeQuery(id+"F5.opPattern","COPY",BODY,{"derivedFrom":makeQuery(id+"F3.opPattern","COPY",BODY,{"derivedFrom":makeQuery(id+"F2.opPattern","COPY",BODY,{"derivedFrom":makeQuery(id+"F1.opRevolve","SWEPT_BODY",BODY,{"disambiguationData":[OSD([sQuery(id+"F0.wireOp",EDGE,"E1")])]}),"instanceName":"1"}),"instanceName":"1"}),"instanceName":"1"}),"instanceName":"1"}),"instanceName":"1"}),"instanceName":"1"}),"instanceName":"1"});
            var Q2708;
            Q2708=makeQuery(id+"F13.opPattern","COPY",BODY,{"derivedFrom":makeQuery(id+"F12.opPattern","COPY",BODY,{"derivedFrom":makeQuery(id+"F11.opPattern","COPY",BODY,{"derivedFrom":makeQuery(id+"F6.opPattern","COPY",BODY,{"derivedFrom":makeQuery(id+"F5.opPattern","COPY",BODY,{"derivedFrom":makeQuery(id+"F4.opPattern","COPY",BODY,{"derivedFrom":makeQuery(id+"F1.opRevolve","SWEPT_BODY",BODY,{"disambiguationData":[OSD([sQuery(id+"F0.wireOp",EDGE,"E1")])]}),"instanceName":"1"}),"instanceName":"1"}),"instanceName":"1"}),"instanceName":"1"}),"instanceName":"1"}),"instanceName":"1"});
            var Q2709;
            Q2709=makeQuery(id+"F13.opPattern","COPY",BODY,{"derivedFrom":makeQuery(id+"F12.opPattern","COPY",BODY,{"derivedFrom":makeQuery(id+"F11.opPattern","COPY",BODY,{"derivedFrom":makeQuery(id+"F6.opPattern","COPY",BODY,{"derivedFrom":makeQuery(id+"F5.opPattern","COPY",BODY,{"derivedFrom":makeQuery(id+"F4.opPattern","COPY",BODY,{"derivedFrom":makeQuery(id+"F2.opPattern","COPY",BODY,{"derivedFrom":makeQuery(id+"F1.opRevolve","SWEPT_BODY",BODY,{"disambiguationData":[OSD([sQuery(id+"F0.wireOp",EDGE,"E1")])]}),"instanceName":"1"}),"instanceName":"1"}),"instanceName":"1"}),"instanceName":"1"}),"instanceName":"1"}),"instanceName":"1"}),"instanceName":"1"});
            var Q2710;
            Q2710=makeQuery(id+"F13.opPattern","COPY",BODY,{"derivedFrom":makeQuery(id+"F12.opPattern","COPY",BODY,{"derivedFrom":makeQuery(id+"F11.opPattern","COPY",BODY,{"derivedFrom":makeQuery(id+"F6.opPattern","COPY",BODY,{"derivedFrom":makeQuery(id+"F5.opPattern","COPY",BODY,{"derivedFrom":makeQuery(id+"F4.opPattern","COPY",BODY,{"derivedFrom":makeQuery(id+"F3.opPattern","COPY",BODY,{"derivedFrom":makeQuery(id+"F2.opPattern","COPY",BODY,{"derivedFrom":makeQuery(id+"F1.opRevolve","SWEPT_BODY",BODY,{"disambiguationData":[OSD([sQuery(id+"F0.wireOp",EDGE,"E1")])]}),"instanceName":"1"}),"instanceName":"1"}),"instanceName":"1"}),"instanceName":"1"}),"instanceName":"1"}),"instanceName":"1"}),"instanceName":"1"}),"instanceName":"1"});
            var Q2711;
            Q2711=makeQuery(id+"F13.opPattern","COPY",BODY,{"derivedFrom":makeQuery(id+"F12.opPattern","COPY",BODY,{"derivedFrom":makeQuery(id+"F11.opPattern","COPY",BODY,{"derivedFrom":makeQuery(id+"F7.opPattern","COPY",BODY,{"derivedFrom":makeQuery(id+"F1.opRevolve","SWEPT_BODY",BODY,{"disambiguationData":[OSD([sQuery(id+"F0.wireOp",EDGE,"E1")])]}),"instanceName":"1"}),"instanceName":"1"}),"instanceName":"1"}),"instanceName":"1"});
            var Q2712;
            Q2712=makeQuery(id+"F13.opPattern","COPY",BODY,{"derivedFrom":makeQuery(id+"F12.opPattern","COPY",BODY,{"derivedFrom":makeQuery(id+"F11.opPattern","COPY",BODY,{"derivedFrom":makeQuery(id+"F7.opPattern","COPY",BODY,{"derivedFrom":makeQuery(id+"F2.opPattern","COPY",BODY,{"derivedFrom":makeQuery(id+"F1.opRevolve","SWEPT_BODY",BODY,{"disambiguationData":[OSD([sQuery(id+"F0.wireOp",EDGE,"E1")])]}),"instanceName":"1"}),"instanceName":"1"}),"instanceName":"1"}),"instanceName":"1"}),"instanceName":"1"});
            var Q2713;
            Q2713=makeQuery(id+"F13.opPattern","COPY",BODY,{"derivedFrom":makeQuery(id+"F12.opPattern","COPY",BODY,{"derivedFrom":makeQuery(id+"F11.opPattern","COPY",BODY,{"derivedFrom":makeQuery(id+"F7.opPattern","COPY",BODY,{"derivedFrom":makeQuery(id+"F3.opPattern","COPY",BODY,{"derivedFrom":makeQuery(id+"F2.opPattern","COPY",BODY,{"derivedFrom":makeQuery(id+"F1.opRevolve","SWEPT_BODY",BODY,{"disambiguationData":[OSD([sQuery(id+"F0.wireOp",EDGE,"E1")])]}),"instanceName":"1"}),"instanceName":"1"}),"instanceName":"1"}),"instanceName":"1"}),"instanceName":"1"}),"instanceName":"1"});
            var Q2714;
            Q2714=makeQuery(id+"F13.opPattern","COPY",BODY,{"derivedFrom":makeQuery(id+"F12.opPattern","COPY",BODY,{"derivedFrom":makeQuery(id+"F11.opPattern","COPY",BODY,{"derivedFrom":makeQuery(id+"F7.opPattern","COPY",BODY,{"derivedFrom":makeQuery(id+"F4.opPattern","COPY",BODY,{"derivedFrom":makeQuery(id+"F1.opRevolve","SWEPT_BODY",BODY,{"disambiguationData":[OSD([sQuery(id+"F0.wireOp",EDGE,"E1")])]}),"instanceName":"1"}),"instanceName":"1"}),"instanceName":"1"}),"instanceName":"1"}),"instanceName":"1"});
            var Q2715;
            Q2715=makeQuery(id+"F13.opPattern","COPY",BODY,{"derivedFrom":makeQuery(id+"F12.opPattern","COPY",BODY,{"derivedFrom":makeQuery(id+"F11.opPattern","COPY",BODY,{"derivedFrom":makeQuery(id+"F7.opPattern","COPY",BODY,{"derivedFrom":makeQuery(id+"F4.opPattern","COPY",BODY,{"derivedFrom":makeQuery(id+"F2.opPattern","COPY",BODY,{"derivedFrom":makeQuery(id+"F1.opRevolve","SWEPT_BODY",BODY,{"disambiguationData":[OSD([sQuery(id+"F0.wireOp",EDGE,"E1")])]}),"instanceName":"1"}),"instanceName":"1"}),"instanceName":"1"}),"instanceName":"1"}),"instanceName":"1"}),"instanceName":"1"});
            var Q2716;
            Q2716=makeQuery(id+"F13.opPattern","COPY",BODY,{"derivedFrom":makeQuery(id+"F12.opPattern","COPY",BODY,{"derivedFrom":makeQuery(id+"F11.opPattern","COPY",BODY,{"derivedFrom":makeQuery(id+"F7.opPattern","COPY",BODY,{"derivedFrom":makeQuery(id+"F4.opPattern","COPY",BODY,{"derivedFrom":makeQuery(id+"F3.opPattern","COPY",BODY,{"derivedFrom":makeQuery(id+"F2.opPattern","COPY",BODY,{"derivedFrom":makeQuery(id+"F1.opRevolve","SWEPT_BODY",BODY,{"disambiguationData":[OSD([sQuery(id+"F0.wireOp",EDGE,"E1")])]}),"instanceName":"1"}),"instanceName":"1"}),"instanceName":"1"}),"instanceName":"1"}),"instanceName":"1"}),"instanceName":"1"}),"instanceName":"1"});
            var Q2717;
            Q2717=makeQuery(id+"F13.opPattern","COPY",BODY,{"derivedFrom":makeQuery(id+"F12.opPattern","COPY",BODY,{"derivedFrom":makeQuery(id+"F11.opPattern","COPY",BODY,{"derivedFrom":makeQuery(id+"F7.opPattern","COPY",BODY,{"derivedFrom":makeQuery(id+"F5.opPattern","COPY",BODY,{"derivedFrom":makeQuery(id+"F1.opRevolve","SWEPT_BODY",BODY,{"disambiguationData":[OSD([sQuery(id+"F0.wireOp",EDGE,"E1")])]}),"instanceName":"1"}),"instanceName":"1"}),"instanceName":"1"}),"instanceName":"1"}),"instanceName":"1"});
            var Q2718;
            Q2718=makeQuery(id+"F13.opPattern","COPY",BODY,{"derivedFrom":makeQuery(id+"F12.opPattern","COPY",BODY,{"derivedFrom":makeQuery(id+"F11.opPattern","COPY",BODY,{"derivedFrom":makeQuery(id+"F7.opPattern","COPY",BODY,{"derivedFrom":makeQuery(id+"F5.opPattern","COPY",BODY,{"derivedFrom":makeQuery(id+"F2.opPattern","COPY",BODY,{"derivedFrom":makeQuery(id+"F1.opRevolve","SWEPT_BODY",BODY,{"disambiguationData":[OSD([sQuery(id+"F0.wireOp",EDGE,"E1")])]}),"instanceName":"1"}),"instanceName":"1"}),"instanceName":"1"}),"instanceName":"1"}),"instanceName":"1"}),"instanceName":"1"});
            var Q2719;
            Q2719=makeQuery(id+"F13.opPattern","COPY",BODY,{"derivedFrom":makeQuery(id+"F12.opPattern","COPY",BODY,{"derivedFrom":makeQuery(id+"F11.opPattern","COPY",BODY,{"derivedFrom":makeQuery(id+"F7.opPattern","COPY",BODY,{"derivedFrom":makeQuery(id+"F5.opPattern","COPY",BODY,{"derivedFrom":makeQuery(id+"F3.opPattern","COPY",BODY,{"derivedFrom":makeQuery(id+"F2.opPattern","COPY",BODY,{"derivedFrom":makeQuery(id+"F1.opRevolve","SWEPT_BODY",BODY,{"disambiguationData":[OSD([sQuery(id+"F0.wireOp",EDGE,"E1")])]}),"instanceName":"1"}),"instanceName":"1"}),"instanceName":"1"}),"instanceName":"1"}),"instanceName":"1"}),"instanceName":"1"}),"instanceName":"1"});
            var Q2720;
            Q2720=makeQuery(id+"F13.opPattern","COPY",BODY,{"derivedFrom":makeQuery(id+"F12.opPattern","COPY",BODY,{"derivedFrom":makeQuery(id+"F11.opPattern","COPY",BODY,{"derivedFrom":makeQuery(id+"F7.opPattern","COPY",BODY,{"derivedFrom":makeQuery(id+"F5.opPattern","COPY",BODY,{"derivedFrom":makeQuery(id+"F4.opPattern","COPY",BODY,{"derivedFrom":makeQuery(id+"F1.opRevolve","SWEPT_BODY",BODY,{"disambiguationData":[OSD([sQuery(id+"F0.wireOp",EDGE,"E1")])]}),"instanceName":"1"}),"instanceName":"1"}),"instanceName":"1"}),"instanceName":"1"}),"instanceName":"1"}),"instanceName":"1"});
            var Q2721;
            Q2721=makeQuery(id+"F13.opPattern","COPY",BODY,{"derivedFrom":makeQuery(id+"F12.opPattern","COPY",BODY,{"derivedFrom":makeQuery(id+"F11.opPattern","COPY",BODY,{"derivedFrom":makeQuery(id+"F7.opPattern","COPY",BODY,{"derivedFrom":makeQuery(id+"F5.opPattern","COPY",BODY,{"derivedFrom":makeQuery(id+"F4.opPattern","COPY",BODY,{"derivedFrom":makeQuery(id+"F2.opPattern","COPY",BODY,{"derivedFrom":makeQuery(id+"F1.opRevolve","SWEPT_BODY",BODY,{"disambiguationData":[OSD([sQuery(id+"F0.wireOp",EDGE,"E1")])]}),"instanceName":"1"}),"instanceName":"1"}),"instanceName":"1"}),"instanceName":"1"}),"instanceName":"1"}),"instanceName":"1"}),"instanceName":"1"});
            var Q2722;
            Q2722=makeQuery(id+"F13.opPattern","COPY",BODY,{"derivedFrom":makeQuery(id+"F12.opPattern","COPY",BODY,{"derivedFrom":makeQuery(id+"F11.opPattern","COPY",BODY,{"derivedFrom":makeQuery(id+"F7.opPattern","COPY",BODY,{"derivedFrom":makeQuery(id+"F5.opPattern","COPY",BODY,{"derivedFrom":makeQuery(id+"F4.opPattern","COPY",BODY,{"derivedFrom":makeQuery(id+"F3.opPattern","COPY",BODY,{"derivedFrom":makeQuery(id+"F2.opPattern","COPY",BODY,{"derivedFrom":makeQuery(id+"F1.opRevolve","SWEPT_BODY",BODY,{"disambiguationData":[OSD([sQuery(id+"F0.wireOp",EDGE,"E1")])]}),"instanceName":"1"}),"instanceName":"1"}),"instanceName":"1"}),"instanceName":"1"}),"instanceName":"1"}),"instanceName":"1"}),"instanceName":"1"}),"instanceName":"1"});
            var Q2723;
            Q2723=makeQuery(id+"F13.opPattern","COPY",BODY,{"derivedFrom":makeQuery(id+"F12.opPattern","COPY",BODY,{"derivedFrom":makeQuery(id+"F11.opPattern","COPY",BODY,{"derivedFrom":makeQuery(id+"F7.opPattern","COPY",BODY,{"derivedFrom":makeQuery(id+"F6.opPattern","COPY",BODY,{"derivedFrom":makeQuery(id+"F1.opRevolve","SWEPT_BODY",BODY,{"disambiguationData":[OSD([sQuery(id+"F0.wireOp",EDGE,"E1")])]}),"instanceName":"1"}),"instanceName":"1"}),"instanceName":"1"}),"instanceName":"1"}),"instanceName":"1"});
            var Q2724;
            Q2724=makeQuery(id+"F13.opPattern","COPY",BODY,{"derivedFrom":makeQuery(id+"F12.opPattern","COPY",BODY,{"derivedFrom":makeQuery(id+"F11.opPattern","COPY",BODY,{"derivedFrom":makeQuery(id+"F7.opPattern","COPY",BODY,{"derivedFrom":makeQuery(id+"F6.opPattern","COPY",BODY,{"derivedFrom":makeQuery(id+"F2.opPattern","COPY",BODY,{"derivedFrom":makeQuery(id+"F1.opRevolve","SWEPT_BODY",BODY,{"disambiguationData":[OSD([sQuery(id+"F0.wireOp",EDGE,"E1")])]}),"instanceName":"1"}),"instanceName":"1"}),"instanceName":"1"}),"instanceName":"1"}),"instanceName":"1"}),"instanceName":"1"});
            var Q2725;
            Q2725=makeQuery(id+"F13.opPattern","COPY",BODY,{"derivedFrom":makeQuery(id+"F12.opPattern","COPY",BODY,{"derivedFrom":makeQuery(id+"F11.opPattern","COPY",BODY,{"derivedFrom":makeQuery(id+"F7.opPattern","COPY",BODY,{"derivedFrom":makeQuery(id+"F6.opPattern","COPY",BODY,{"derivedFrom":makeQuery(id+"F3.opPattern","COPY",BODY,{"derivedFrom":makeQuery(id+"F2.opPattern","COPY",BODY,{"derivedFrom":makeQuery(id+"F1.opRevolve","SWEPT_BODY",BODY,{"disambiguationData":[OSD([sQuery(id+"F0.wireOp",EDGE,"E1")])]}),"instanceName":"1"}),"instanceName":"1"}),"instanceName":"1"}),"instanceName":"1"}),"instanceName":"1"}),"instanceName":"1"}),"instanceName":"1"});
            var Q2726;
            Q2726=makeQuery(id+"F13.opPattern","COPY",BODY,{"derivedFrom":makeQuery(id+"F12.opPattern","COPY",BODY,{"derivedFrom":makeQuery(id+"F11.opPattern","COPY",BODY,{"derivedFrom":makeQuery(id+"F7.opPattern","COPY",BODY,{"derivedFrom":makeQuery(id+"F6.opPattern","COPY",BODY,{"derivedFrom":makeQuery(id+"F4.opPattern","COPY",BODY,{"derivedFrom":makeQuery(id+"F1.opRevolve","SWEPT_BODY",BODY,{"disambiguationData":[OSD([sQuery(id+"F0.wireOp",EDGE,"E1")])]}),"instanceName":"1"}),"instanceName":"1"}),"instanceName":"1"}),"instanceName":"1"}),"instanceName":"1"}),"instanceName":"1"});
            var Q2727;
            Q2727=makeQuery(id+"F13.opPattern","COPY",BODY,{"derivedFrom":makeQuery(id+"F12.opPattern","COPY",BODY,{"derivedFrom":makeQuery(id+"F11.opPattern","COPY",BODY,{"derivedFrom":makeQuery(id+"F7.opPattern","COPY",BODY,{"derivedFrom":makeQuery(id+"F6.opPattern","COPY",BODY,{"derivedFrom":makeQuery(id+"F4.opPattern","COPY",BODY,{"derivedFrom":makeQuery(id+"F2.opPattern","COPY",BODY,{"derivedFrom":makeQuery(id+"F1.opRevolve","SWEPT_BODY",BODY,{"disambiguationData":[OSD([sQuery(id+"F0.wireOp",EDGE,"E1")])]}),"instanceName":"1"}),"instanceName":"1"}),"instanceName":"1"}),"instanceName":"1"}),"instanceName":"1"}),"instanceName":"1"}),"instanceName":"1"});
            var Q2728;
            Q2728=makeQuery(id+"F13.opPattern","COPY",BODY,{"derivedFrom":makeQuery(id+"F12.opPattern","COPY",BODY,{"derivedFrom":makeQuery(id+"F11.opPattern","COPY",BODY,{"derivedFrom":makeQuery(id+"F7.opPattern","COPY",BODY,{"derivedFrom":makeQuery(id+"F6.opPattern","COPY",BODY,{"derivedFrom":makeQuery(id+"F4.opPattern","COPY",BODY,{"derivedFrom":makeQuery(id+"F3.opPattern","COPY",BODY,{"derivedFrom":makeQuery(id+"F2.opPattern","COPY",BODY,{"derivedFrom":makeQuery(id+"F1.opRevolve","SWEPT_BODY",BODY,{"disambiguationData":[OSD([sQuery(id+"F0.wireOp",EDGE,"E1")])]}),"instanceName":"1"}),"instanceName":"1"}),"instanceName":"1"}),"instanceName":"1"}),"instanceName":"1"}),"instanceName":"1"}),"instanceName":"1"}),"instanceName":"1"});
            var Q2729;
            Q2729=makeQuery(id+"F13.opPattern","COPY",BODY,{"derivedFrom":makeQuery(id+"F12.opPattern","COPY",BODY,{"derivedFrom":makeQuery(id+"F11.opPattern","COPY",BODY,{"derivedFrom":makeQuery(id+"F7.opPattern","COPY",BODY,{"derivedFrom":makeQuery(id+"F6.opPattern","COPY",BODY,{"derivedFrom":makeQuery(id+"F5.opPattern","COPY",BODY,{"derivedFrom":makeQuery(id+"F1.opRevolve","SWEPT_BODY",BODY,{"disambiguationData":[OSD([sQuery(id+"F0.wireOp",EDGE,"E1")])]}),"instanceName":"1"}),"instanceName":"1"}),"instanceName":"1"}),"instanceName":"1"}),"instanceName":"1"}),"instanceName":"1"});
            var Q2730;
            Q2730=makeQuery(id+"F13.opPattern","COPY",BODY,{"derivedFrom":makeQuery(id+"F12.opPattern","COPY",BODY,{"derivedFrom":makeQuery(id+"F11.opPattern","COPY",BODY,{"derivedFrom":makeQuery(id+"F7.opPattern","COPY",BODY,{"derivedFrom":makeQuery(id+"F6.opPattern","COPY",BODY,{"derivedFrom":makeQuery(id+"F5.opPattern","COPY",BODY,{"derivedFrom":makeQuery(id+"F2.opPattern","COPY",BODY,{"derivedFrom":makeQuery(id+"F1.opRevolve","SWEPT_BODY",BODY,{"disambiguationData":[OSD([sQuery(id+"F0.wireOp",EDGE,"E1")])]}),"instanceName":"1"}),"instanceName":"1"}),"instanceName":"1"}),"instanceName":"1"}),"instanceName":"1"}),"instanceName":"1"}),"instanceName":"1"});
            var Q2731;
            Q2731=makeQuery(id+"F13.opPattern","COPY",BODY,{"derivedFrom":makeQuery(id+"F12.opPattern","COPY",BODY,{"derivedFrom":makeQuery(id+"F11.opPattern","COPY",BODY,{"derivedFrom":makeQuery(id+"F7.opPattern","COPY",BODY,{"derivedFrom":makeQuery(id+"F6.opPattern","COPY",BODY,{"derivedFrom":makeQuery(id+"F5.opPattern","COPY",BODY,{"derivedFrom":makeQuery(id+"F3.opPattern","COPY",BODY,{"derivedFrom":makeQuery(id+"F2.opPattern","COPY",BODY,{"derivedFrom":makeQuery(id+"F1.opRevolve","SWEPT_BODY",BODY,{"disambiguationData":[OSD([sQuery(id+"F0.wireOp",EDGE,"E1")])]}),"instanceName":"1"}),"instanceName":"1"}),"instanceName":"1"}),"instanceName":"1"}),"instanceName":"1"}),"instanceName":"1"}),"instanceName":"1"}),"instanceName":"1"});
            var Q2732;
            Q2732=makeQuery(id+"F13.opPattern","COPY",BODY,{"derivedFrom":makeQuery(id+"F12.opPattern","COPY",BODY,{"derivedFrom":makeQuery(id+"F11.opPattern","COPY",BODY,{"derivedFrom":makeQuery(id+"F7.opPattern","COPY",BODY,{"derivedFrom":makeQuery(id+"F6.opPattern","COPY",BODY,{"derivedFrom":makeQuery(id+"F5.opPattern","COPY",BODY,{"derivedFrom":makeQuery(id+"F4.opPattern","COPY",BODY,{"derivedFrom":makeQuery(id+"F1.opRevolve","SWEPT_BODY",BODY,{"disambiguationData":[OSD([sQuery(id+"F0.wireOp",EDGE,"E1")])]}),"instanceName":"1"}),"instanceName":"1"}),"instanceName":"1"}),"instanceName":"1"}),"instanceName":"1"}),"instanceName":"1"}),"instanceName":"1"});
            var Q2733;
            Q2733=makeQuery(id+"F13.opPattern","COPY",BODY,{"derivedFrom":makeQuery(id+"F12.opPattern","COPY",BODY,{"derivedFrom":makeQuery(id+"F11.opPattern","COPY",BODY,{"derivedFrom":makeQuery(id+"F7.opPattern","COPY",BODY,{"derivedFrom":makeQuery(id+"F6.opPattern","COPY",BODY,{"derivedFrom":makeQuery(id+"F5.opPattern","COPY",BODY,{"derivedFrom":makeQuery(id+"F4.opPattern","COPY",BODY,{"derivedFrom":makeQuery(id+"F2.opPattern","COPY",BODY,{"derivedFrom":makeQuery(id+"F1.opRevolve","SWEPT_BODY",BODY,{"disambiguationData":[OSD([sQuery(id+"F0.wireOp",EDGE,"E1")])]}),"instanceName":"1"}),"instanceName":"1"}),"instanceName":"1"}),"instanceName":"1"}),"instanceName":"1"}),"instanceName":"1"}),"instanceName":"1"}),"instanceName":"1"});
            var Q2734;
            Q2734=makeQuery(id+"F13.opPattern","COPY",BODY,{"derivedFrom":makeQuery(id+"F12.opPattern","COPY",BODY,{"derivedFrom":makeQuery(id+"F11.opPattern","COPY",BODY,{"derivedFrom":makeQuery(id+"F7.opPattern","COPY",BODY,{"derivedFrom":makeQuery(id+"F6.opPattern","COPY",BODY,{"derivedFrom":makeQuery(id+"F5.opPattern","COPY",BODY,{"derivedFrom":makeQuery(id+"F4.opPattern","COPY",BODY,{"derivedFrom":makeQuery(id+"F3.opPattern","COPY",BODY,{"derivedFrom":makeQuery(id+"F2.opPattern","COPY",BODY,{"derivedFrom":makeQuery(id+"F1.opRevolve","SWEPT_BODY",BODY,{"disambiguationData":[OSD([sQuery(id+"F0.wireOp",EDGE,"E1")])]}),"instanceName":"1"}),"instanceName":"1"}),"instanceName":"1"}),"instanceName":"1"}),"instanceName":"1"}),"instanceName":"1"}),"instanceName":"1"}),"instanceName":"1"}),"instanceName":"1"});
            var Q2735;
            Q2735=makeQuery(id+"F13.opPattern","COPY",BODY,{"derivedFrom":makeQuery(id+"F12.opPattern","COPY",BODY,{"derivedFrom":makeQuery(id+"F11.opPattern","COPY",BODY,{"derivedFrom":makeQuery(id+"F8.opPattern","COPY",BODY,{"derivedFrom":makeQuery(id+"F1.opRevolve","SWEPT_BODY",BODY,{"disambiguationData":[OSD([sQuery(id+"F0.wireOp",EDGE,"E1")])]}),"instanceName":"1"}),"instanceName":"1"}),"instanceName":"1"}),"instanceName":"1"});
            var Q2736;
            Q2736=makeQuery(id+"F13.opPattern","COPY",BODY,{"derivedFrom":makeQuery(id+"F12.opPattern","COPY",BODY,{"derivedFrom":makeQuery(id+"F11.opPattern","COPY",BODY,{"derivedFrom":makeQuery(id+"F8.opPattern","COPY",BODY,{"derivedFrom":makeQuery(id+"F2.opPattern","COPY",BODY,{"derivedFrom":makeQuery(id+"F1.opRevolve","SWEPT_BODY",BODY,{"disambiguationData":[OSD([sQuery(id+"F0.wireOp",EDGE,"E1")])]}),"instanceName":"1"}),"instanceName":"1"}),"instanceName":"1"}),"instanceName":"1"}),"instanceName":"1"});
            var Q2737;
            Q2737=makeQuery(id+"F13.opPattern","COPY",BODY,{"derivedFrom":makeQuery(id+"F12.opPattern","COPY",BODY,{"derivedFrom":makeQuery(id+"F11.opPattern","COPY",BODY,{"derivedFrom":makeQuery(id+"F8.opPattern","COPY",BODY,{"derivedFrom":makeQuery(id+"F3.opPattern","COPY",BODY,{"derivedFrom":makeQuery(id+"F2.opPattern","COPY",BODY,{"derivedFrom":makeQuery(id+"F1.opRevolve","SWEPT_BODY",BODY,{"disambiguationData":[OSD([sQuery(id+"F0.wireOp",EDGE,"E1")])]}),"instanceName":"1"}),"instanceName":"1"}),"instanceName":"1"}),"instanceName":"1"}),"instanceName":"1"}),"instanceName":"1"});
            var Q2738;
            Q2738=makeQuery(id+"F13.opPattern","COPY",BODY,{"derivedFrom":makeQuery(id+"F12.opPattern","COPY",BODY,{"derivedFrom":makeQuery(id+"F11.opPattern","COPY",BODY,{"derivedFrom":makeQuery(id+"F8.opPattern","COPY",BODY,{"derivedFrom":makeQuery(id+"F4.opPattern","COPY",BODY,{"derivedFrom":makeQuery(id+"F1.opRevolve","SWEPT_BODY",BODY,{"disambiguationData":[OSD([sQuery(id+"F0.wireOp",EDGE,"E1")])]}),"instanceName":"1"}),"instanceName":"1"}),"instanceName":"1"}),"instanceName":"1"}),"instanceName":"1"});
            var Q2739;
            Q2739=makeQuery(id+"F13.opPattern","COPY",BODY,{"derivedFrom":makeQuery(id+"F12.opPattern","COPY",BODY,{"derivedFrom":makeQuery(id+"F11.opPattern","COPY",BODY,{"derivedFrom":makeQuery(id+"F8.opPattern","COPY",BODY,{"derivedFrom":makeQuery(id+"F4.opPattern","COPY",BODY,{"derivedFrom":makeQuery(id+"F2.opPattern","COPY",BODY,{"derivedFrom":makeQuery(id+"F1.opRevolve","SWEPT_BODY",BODY,{"disambiguationData":[OSD([sQuery(id+"F0.wireOp",EDGE,"E1")])]}),"instanceName":"1"}),"instanceName":"1"}),"instanceName":"1"}),"instanceName":"1"}),"instanceName":"1"}),"instanceName":"1"});
            var Q2740;
            Q2740=makeQuery(id+"F13.opPattern","COPY",BODY,{"derivedFrom":makeQuery(id+"F12.opPattern","COPY",BODY,{"derivedFrom":makeQuery(id+"F11.opPattern","COPY",BODY,{"derivedFrom":makeQuery(id+"F8.opPattern","COPY",BODY,{"derivedFrom":makeQuery(id+"F4.opPattern","COPY",BODY,{"derivedFrom":makeQuery(id+"F3.opPattern","COPY",BODY,{"derivedFrom":makeQuery(id+"F2.opPattern","COPY",BODY,{"derivedFrom":makeQuery(id+"F1.opRevolve","SWEPT_BODY",BODY,{"disambiguationData":[OSD([sQuery(id+"F0.wireOp",EDGE,"E1")])]}),"instanceName":"1"}),"instanceName":"1"}),"instanceName":"1"}),"instanceName":"1"}),"instanceName":"1"}),"instanceName":"1"}),"instanceName":"1"});
            var Q2741;
            Q2741=makeQuery(id+"F13.opPattern","COPY",BODY,{"derivedFrom":makeQuery(id+"F12.opPattern","COPY",BODY,{"derivedFrom":makeQuery(id+"F11.opPattern","COPY",BODY,{"derivedFrom":makeQuery(id+"F8.opPattern","COPY",BODY,{"derivedFrom":makeQuery(id+"F5.opPattern","COPY",BODY,{"derivedFrom":makeQuery(id+"F1.opRevolve","SWEPT_BODY",BODY,{"disambiguationData":[OSD([sQuery(id+"F0.wireOp",EDGE,"E1")])]}),"instanceName":"1"}),"instanceName":"1"}),"instanceName":"1"}),"instanceName":"1"}),"instanceName":"1"});
            var Q2742;
            Q2742=makeQuery(id+"F13.opPattern","COPY",BODY,{"derivedFrom":makeQuery(id+"F12.opPattern","COPY",BODY,{"derivedFrom":makeQuery(id+"F11.opPattern","COPY",BODY,{"derivedFrom":makeQuery(id+"F8.opPattern","COPY",BODY,{"derivedFrom":makeQuery(id+"F5.opPattern","COPY",BODY,{"derivedFrom":makeQuery(id+"F2.opPattern","COPY",BODY,{"derivedFrom":makeQuery(id+"F1.opRevolve","SWEPT_BODY",BODY,{"disambiguationData":[OSD([sQuery(id+"F0.wireOp",EDGE,"E1")])]}),"instanceName":"1"}),"instanceName":"1"}),"instanceName":"1"}),"instanceName":"1"}),"instanceName":"1"}),"instanceName":"1"});
            var Q2743;
            Q2743=makeQuery(id+"F13.opPattern","COPY",BODY,{"derivedFrom":makeQuery(id+"F12.opPattern","COPY",BODY,{"derivedFrom":makeQuery(id+"F11.opPattern","COPY",BODY,{"derivedFrom":makeQuery(id+"F8.opPattern","COPY",BODY,{"derivedFrom":makeQuery(id+"F5.opPattern","COPY",BODY,{"derivedFrom":makeQuery(id+"F3.opPattern","COPY",BODY,{"derivedFrom":makeQuery(id+"F2.opPattern","COPY",BODY,{"derivedFrom":makeQuery(id+"F1.opRevolve","SWEPT_BODY",BODY,{"disambiguationData":[OSD([sQuery(id+"F0.wireOp",EDGE,"E1")])]}),"instanceName":"1"}),"instanceName":"1"}),"instanceName":"1"}),"instanceName":"1"}),"instanceName":"1"}),"instanceName":"1"}),"instanceName":"1"});
            var Q2744;
            Q2744=makeQuery(id+"F13.opPattern","COPY",BODY,{"derivedFrom":makeQuery(id+"F12.opPattern","COPY",BODY,{"derivedFrom":makeQuery(id+"F11.opPattern","COPY",BODY,{"derivedFrom":makeQuery(id+"F8.opPattern","COPY",BODY,{"derivedFrom":makeQuery(id+"F5.opPattern","COPY",BODY,{"derivedFrom":makeQuery(id+"F4.opPattern","COPY",BODY,{"derivedFrom":makeQuery(id+"F1.opRevolve","SWEPT_BODY",BODY,{"disambiguationData":[OSD([sQuery(id+"F0.wireOp",EDGE,"E1")])]}),"instanceName":"1"}),"instanceName":"1"}),"instanceName":"1"}),"instanceName":"1"}),"instanceName":"1"}),"instanceName":"1"});
            var Q2745;
            Q2745=makeQuery(id+"F13.opPattern","COPY",BODY,{"derivedFrom":makeQuery(id+"F12.opPattern","COPY",BODY,{"derivedFrom":makeQuery(id+"F11.opPattern","COPY",BODY,{"derivedFrom":makeQuery(id+"F8.opPattern","COPY",BODY,{"derivedFrom":makeQuery(id+"F5.opPattern","COPY",BODY,{"derivedFrom":makeQuery(id+"F4.opPattern","COPY",BODY,{"derivedFrom":makeQuery(id+"F2.opPattern","COPY",BODY,{"derivedFrom":makeQuery(id+"F1.opRevolve","SWEPT_BODY",BODY,{"disambiguationData":[OSD([sQuery(id+"F0.wireOp",EDGE,"E1")])]}),"instanceName":"1"}),"instanceName":"1"}),"instanceName":"1"}),"instanceName":"1"}),"instanceName":"1"}),"instanceName":"1"}),"instanceName":"1"});
            var Q2746;
            Q2746=makeQuery(id+"F13.opPattern","COPY",BODY,{"derivedFrom":makeQuery(id+"F12.opPattern","COPY",BODY,{"derivedFrom":makeQuery(id+"F11.opPattern","COPY",BODY,{"derivedFrom":makeQuery(id+"F8.opPattern","COPY",BODY,{"derivedFrom":makeQuery(id+"F5.opPattern","COPY",BODY,{"derivedFrom":makeQuery(id+"F4.opPattern","COPY",BODY,{"derivedFrom":makeQuery(id+"F3.opPattern","COPY",BODY,{"derivedFrom":makeQuery(id+"F2.opPattern","COPY",BODY,{"derivedFrom":makeQuery(id+"F1.opRevolve","SWEPT_BODY",BODY,{"disambiguationData":[OSD([sQuery(id+"F0.wireOp",EDGE,"E1")])]}),"instanceName":"1"}),"instanceName":"1"}),"instanceName":"1"}),"instanceName":"1"}),"instanceName":"1"}),"instanceName":"1"}),"instanceName":"1"}),"instanceName":"1"});
            var Q2747;
            Q2747=makeQuery(id+"F13.opPattern","COPY",BODY,{"derivedFrom":makeQuery(id+"F12.opPattern","COPY",BODY,{"derivedFrom":makeQuery(id+"F11.opPattern","COPY",BODY,{"derivedFrom":makeQuery(id+"F8.opPattern","COPY",BODY,{"derivedFrom":makeQuery(id+"F6.opPattern","COPY",BODY,{"derivedFrom":makeQuery(id+"F1.opRevolve","SWEPT_BODY",BODY,{"disambiguationData":[OSD([sQuery(id+"F0.wireOp",EDGE,"E1")])]}),"instanceName":"1"}),"instanceName":"1"}),"instanceName":"1"}),"instanceName":"1"}),"instanceName":"1"});
            var Q2748;
            Q2748=makeQuery(id+"F13.opPattern","COPY",BODY,{"derivedFrom":makeQuery(id+"F12.opPattern","COPY",BODY,{"derivedFrom":makeQuery(id+"F11.opPattern","COPY",BODY,{"derivedFrom":makeQuery(id+"F8.opPattern","COPY",BODY,{"derivedFrom":makeQuery(id+"F6.opPattern","COPY",BODY,{"derivedFrom":makeQuery(id+"F2.opPattern","COPY",BODY,{"derivedFrom":makeQuery(id+"F1.opRevolve","SWEPT_BODY",BODY,{"disambiguationData":[OSD([sQuery(id+"F0.wireOp",EDGE,"E1")])]}),"instanceName":"1"}),"instanceName":"1"}),"instanceName":"1"}),"instanceName":"1"}),"instanceName":"1"}),"instanceName":"1"});
            var Q2749;
            Q2749=makeQuery(id+"F13.opPattern","COPY",BODY,{"derivedFrom":makeQuery(id+"F12.opPattern","COPY",BODY,{"derivedFrom":makeQuery(id+"F11.opPattern","COPY",BODY,{"derivedFrom":makeQuery(id+"F8.opPattern","COPY",BODY,{"derivedFrom":makeQuery(id+"F6.opPattern","COPY",BODY,{"derivedFrom":makeQuery(id+"F3.opPattern","COPY",BODY,{"derivedFrom":makeQuery(id+"F2.opPattern","COPY",BODY,{"derivedFrom":makeQuery(id+"F1.opRevolve","SWEPT_BODY",BODY,{"disambiguationData":[OSD([sQuery(id+"F0.wireOp",EDGE,"E1")])]}),"instanceName":"1"}),"instanceName":"1"}),"instanceName":"1"}),"instanceName":"1"}),"instanceName":"1"}),"instanceName":"1"}),"instanceName":"1"});
            var Q2750;
            Q2750=makeQuery(id+"F13.opPattern","COPY",BODY,{"derivedFrom":makeQuery(id+"F12.opPattern","COPY",BODY,{"derivedFrom":makeQuery(id+"F11.opPattern","COPY",BODY,{"derivedFrom":makeQuery(id+"F8.opPattern","COPY",BODY,{"derivedFrom":makeQuery(id+"F6.opPattern","COPY",BODY,{"derivedFrom":makeQuery(id+"F4.opPattern","COPY",BODY,{"derivedFrom":makeQuery(id+"F1.opRevolve","SWEPT_BODY",BODY,{"disambiguationData":[OSD([sQuery(id+"F0.wireOp",EDGE,"E1")])]}),"instanceName":"1"}),"instanceName":"1"}),"instanceName":"1"}),"instanceName":"1"}),"instanceName":"1"}),"instanceName":"1"});
            var Q2751;
            Q2751=makeQuery(id+"F13.opPattern","COPY",BODY,{"derivedFrom":makeQuery(id+"F12.opPattern","COPY",BODY,{"derivedFrom":makeQuery(id+"F11.opPattern","COPY",BODY,{"derivedFrom":makeQuery(id+"F8.opPattern","COPY",BODY,{"derivedFrom":makeQuery(id+"F6.opPattern","COPY",BODY,{"derivedFrom":makeQuery(id+"F4.opPattern","COPY",BODY,{"derivedFrom":makeQuery(id+"F2.opPattern","COPY",BODY,{"derivedFrom":makeQuery(id+"F1.opRevolve","SWEPT_BODY",BODY,{"disambiguationData":[OSD([sQuery(id+"F0.wireOp",EDGE,"E1")])]}),"instanceName":"1"}),"instanceName":"1"}),"instanceName":"1"}),"instanceName":"1"}),"instanceName":"1"}),"instanceName":"1"}),"instanceName":"1"});
            var Q2752;
            Q2752=makeQuery(id+"F13.opPattern","COPY",BODY,{"derivedFrom":makeQuery(id+"F12.opPattern","COPY",BODY,{"derivedFrom":makeQuery(id+"F11.opPattern","COPY",BODY,{"derivedFrom":makeQuery(id+"F8.opPattern","COPY",BODY,{"derivedFrom":makeQuery(id+"F6.opPattern","COPY",BODY,{"derivedFrom":makeQuery(id+"F4.opPattern","COPY",BODY,{"derivedFrom":makeQuery(id+"F3.opPattern","COPY",BODY,{"derivedFrom":makeQuery(id+"F2.opPattern","COPY",BODY,{"derivedFrom":makeQuery(id+"F1.opRevolve","SWEPT_BODY",BODY,{"disambiguationData":[OSD([sQuery(id+"F0.wireOp",EDGE,"E1")])]}),"instanceName":"1"}),"instanceName":"1"}),"instanceName":"1"}),"instanceName":"1"}),"instanceName":"1"}),"instanceName":"1"}),"instanceName":"1"}),"instanceName":"1"});
            var Q2753;
            Q2753=makeQuery(id+"F13.opPattern","COPY",BODY,{"derivedFrom":makeQuery(id+"F12.opPattern","COPY",BODY,{"derivedFrom":makeQuery(id+"F11.opPattern","COPY",BODY,{"derivedFrom":makeQuery(id+"F8.opPattern","COPY",BODY,{"derivedFrom":makeQuery(id+"F6.opPattern","COPY",BODY,{"derivedFrom":makeQuery(id+"F5.opPattern","COPY",BODY,{"derivedFrom":makeQuery(id+"F1.opRevolve","SWEPT_BODY",BODY,{"disambiguationData":[OSD([sQuery(id+"F0.wireOp",EDGE,"E1")])]}),"instanceName":"1"}),"instanceName":"1"}),"instanceName":"1"}),"instanceName":"1"}),"instanceName":"1"}),"instanceName":"1"});
            var Q2754;
            Q2754=makeQuery(id+"F13.opPattern","COPY",BODY,{"derivedFrom":makeQuery(id+"F12.opPattern","COPY",BODY,{"derivedFrom":makeQuery(id+"F11.opPattern","COPY",BODY,{"derivedFrom":makeQuery(id+"F8.opPattern","COPY",BODY,{"derivedFrom":makeQuery(id+"F6.opPattern","COPY",BODY,{"derivedFrom":makeQuery(id+"F5.opPattern","COPY",BODY,{"derivedFrom":makeQuery(id+"F2.opPattern","COPY",BODY,{"derivedFrom":makeQuery(id+"F1.opRevolve","SWEPT_BODY",BODY,{"disambiguationData":[OSD([sQuery(id+"F0.wireOp",EDGE,"E1")])]}),"instanceName":"1"}),"instanceName":"1"}),"instanceName":"1"}),"instanceName":"1"}),"instanceName":"1"}),"instanceName":"1"}),"instanceName":"1"});
            var Q2755;
            Q2755=makeQuery(id+"F13.opPattern","COPY",BODY,{"derivedFrom":makeQuery(id+"F12.opPattern","COPY",BODY,{"derivedFrom":makeQuery(id+"F11.opPattern","COPY",BODY,{"derivedFrom":makeQuery(id+"F8.opPattern","COPY",BODY,{"derivedFrom":makeQuery(id+"F6.opPattern","COPY",BODY,{"derivedFrom":makeQuery(id+"F5.opPattern","COPY",BODY,{"derivedFrom":makeQuery(id+"F3.opPattern","COPY",BODY,{"derivedFrom":makeQuery(id+"F2.opPattern","COPY",BODY,{"derivedFrom":makeQuery(id+"F1.opRevolve","SWEPT_BODY",BODY,{"disambiguationData":[OSD([sQuery(id+"F0.wireOp",EDGE,"E1")])]}),"instanceName":"1"}),"instanceName":"1"}),"instanceName":"1"}),"instanceName":"1"}),"instanceName":"1"}),"instanceName":"1"}),"instanceName":"1"}),"instanceName":"1"});
            var Q2756;
            Q2756=makeQuery(id+"F13.opPattern","COPY",BODY,{"derivedFrom":makeQuery(id+"F12.opPattern","COPY",BODY,{"derivedFrom":makeQuery(id+"F11.opPattern","COPY",BODY,{"derivedFrom":makeQuery(id+"F8.opPattern","COPY",BODY,{"derivedFrom":makeQuery(id+"F6.opPattern","COPY",BODY,{"derivedFrom":makeQuery(id+"F5.opPattern","COPY",BODY,{"derivedFrom":makeQuery(id+"F4.opPattern","COPY",BODY,{"derivedFrom":makeQuery(id+"F1.opRevolve","SWEPT_BODY",BODY,{"disambiguationData":[OSD([sQuery(id+"F0.wireOp",EDGE,"E1")])]}),"instanceName":"1"}),"instanceName":"1"}),"instanceName":"1"}),"instanceName":"1"}),"instanceName":"1"}),"instanceName":"1"}),"instanceName":"1"});
            var Q2757;
            Q2757=makeQuery(id+"F13.opPattern","COPY",BODY,{"derivedFrom":makeQuery(id+"F12.opPattern","COPY",BODY,{"derivedFrom":makeQuery(id+"F11.opPattern","COPY",BODY,{"derivedFrom":makeQuery(id+"F8.opPattern","COPY",BODY,{"derivedFrom":makeQuery(id+"F6.opPattern","COPY",BODY,{"derivedFrom":makeQuery(id+"F5.opPattern","COPY",BODY,{"derivedFrom":makeQuery(id+"F4.opPattern","COPY",BODY,{"derivedFrom":makeQuery(id+"F2.opPattern","COPY",BODY,{"derivedFrom":makeQuery(id+"F1.opRevolve","SWEPT_BODY",BODY,{"disambiguationData":[OSD([sQuery(id+"F0.wireOp",EDGE,"E1")])]}),"instanceName":"1"}),"instanceName":"1"}),"instanceName":"1"}),"instanceName":"1"}),"instanceName":"1"}),"instanceName":"1"}),"instanceName":"1"}),"instanceName":"1"});
            var Q2758;
            Q2758=makeQuery(id+"F13.opPattern","COPY",BODY,{"derivedFrom":makeQuery(id+"F12.opPattern","COPY",BODY,{"derivedFrom":makeQuery(id+"F11.opPattern","COPY",BODY,{"derivedFrom":makeQuery(id+"F8.opPattern","COPY",BODY,{"derivedFrom":makeQuery(id+"F6.opPattern","COPY",BODY,{"derivedFrom":makeQuery(id+"F5.opPattern","COPY",BODY,{"derivedFrom":makeQuery(id+"F4.opPattern","COPY",BODY,{"derivedFrom":makeQuery(id+"F3.opPattern","COPY",BODY,{"derivedFrom":makeQuery(id+"F2.opPattern","COPY",BODY,{"derivedFrom":makeQuery(id+"F1.opRevolve","SWEPT_BODY",BODY,{"disambiguationData":[OSD([sQuery(id+"F0.wireOp",EDGE,"E1")])]}),"instanceName":"1"}),"instanceName":"1"}),"instanceName":"1"}),"instanceName":"1"}),"instanceName":"1"}),"instanceName":"1"}),"instanceName":"1"}),"instanceName":"1"}),"instanceName":"1"});
            var Q2759;
            Q2759=makeQuery(id+"F13.opPattern","COPY",BODY,{"derivedFrom":makeQuery(id+"F12.opPattern","COPY",BODY,{"derivedFrom":makeQuery(id+"F11.opPattern","COPY",BODY,{"derivedFrom":makeQuery(id+"F8.opPattern","COPY",BODY,{"derivedFrom":makeQuery(id+"F7.opPattern","COPY",BODY,{"derivedFrom":makeQuery(id+"F1.opRevolve","SWEPT_BODY",BODY,{"disambiguationData":[OSD([sQuery(id+"F0.wireOp",EDGE,"E1")])]}),"instanceName":"1"}),"instanceName":"1"}),"instanceName":"1"}),"instanceName":"1"}),"instanceName":"1"});
            var Q2760;
            Q2760=makeQuery(id+"F13.opPattern","COPY",BODY,{"derivedFrom":makeQuery(id+"F12.opPattern","COPY",BODY,{"derivedFrom":makeQuery(id+"F11.opPattern","COPY",BODY,{"derivedFrom":makeQuery(id+"F8.opPattern","COPY",BODY,{"derivedFrom":makeQuery(id+"F7.opPattern","COPY",BODY,{"derivedFrom":makeQuery(id+"F2.opPattern","COPY",BODY,{"derivedFrom":makeQuery(id+"F1.opRevolve","SWEPT_BODY",BODY,{"disambiguationData":[OSD([sQuery(id+"F0.wireOp",EDGE,"E1")])]}),"instanceName":"1"}),"instanceName":"1"}),"instanceName":"1"}),"instanceName":"1"}),"instanceName":"1"}),"instanceName":"1"});
            var Q2761;
            Q2761=makeQuery(id+"F13.opPattern","COPY",BODY,{"derivedFrom":makeQuery(id+"F12.opPattern","COPY",BODY,{"derivedFrom":makeQuery(id+"F11.opPattern","COPY",BODY,{"derivedFrom":makeQuery(id+"F8.opPattern","COPY",BODY,{"derivedFrom":makeQuery(id+"F7.opPattern","COPY",BODY,{"derivedFrom":makeQuery(id+"F3.opPattern","COPY",BODY,{"derivedFrom":makeQuery(id+"F2.opPattern","COPY",BODY,{"derivedFrom":makeQuery(id+"F1.opRevolve","SWEPT_BODY",BODY,{"disambiguationData":[OSD([sQuery(id+"F0.wireOp",EDGE,"E1")])]}),"instanceName":"1"}),"instanceName":"1"}),"instanceName":"1"}),"instanceName":"1"}),"instanceName":"1"}),"instanceName":"1"}),"instanceName":"1"});
            var Q2762;
            Q2762=makeQuery(id+"F13.opPattern","COPY",BODY,{"derivedFrom":makeQuery(id+"F12.opPattern","COPY",BODY,{"derivedFrom":makeQuery(id+"F11.opPattern","COPY",BODY,{"derivedFrom":makeQuery(id+"F8.opPattern","COPY",BODY,{"derivedFrom":makeQuery(id+"F7.opPattern","COPY",BODY,{"derivedFrom":makeQuery(id+"F4.opPattern","COPY",BODY,{"derivedFrom":makeQuery(id+"F1.opRevolve","SWEPT_BODY",BODY,{"disambiguationData":[OSD([sQuery(id+"F0.wireOp",EDGE,"E1")])]}),"instanceName":"1"}),"instanceName":"1"}),"instanceName":"1"}),"instanceName":"1"}),"instanceName":"1"}),"instanceName":"1"});
            var Q2763;
            Q2763=makeQuery(id+"F13.opPattern","COPY",BODY,{"derivedFrom":makeQuery(id+"F12.opPattern","COPY",BODY,{"derivedFrom":makeQuery(id+"F11.opPattern","COPY",BODY,{"derivedFrom":makeQuery(id+"F8.opPattern","COPY",BODY,{"derivedFrom":makeQuery(id+"F7.opPattern","COPY",BODY,{"derivedFrom":makeQuery(id+"F4.opPattern","COPY",BODY,{"derivedFrom":makeQuery(id+"F2.opPattern","COPY",BODY,{"derivedFrom":makeQuery(id+"F1.opRevolve","SWEPT_BODY",BODY,{"disambiguationData":[OSD([sQuery(id+"F0.wireOp",EDGE,"E1")])]}),"instanceName":"1"}),"instanceName":"1"}),"instanceName":"1"}),"instanceName":"1"}),"instanceName":"1"}),"instanceName":"1"}),"instanceName":"1"});
            var Q2764;
            Q2764=makeQuery(id+"F13.opPattern","COPY",BODY,{"derivedFrom":makeQuery(id+"F12.opPattern","COPY",BODY,{"derivedFrom":makeQuery(id+"F11.opPattern","COPY",BODY,{"derivedFrom":makeQuery(id+"F8.opPattern","COPY",BODY,{"derivedFrom":makeQuery(id+"F7.opPattern","COPY",BODY,{"derivedFrom":makeQuery(id+"F4.opPattern","COPY",BODY,{"derivedFrom":makeQuery(id+"F3.opPattern","COPY",BODY,{"derivedFrom":makeQuery(id+"F2.opPattern","COPY",BODY,{"derivedFrom":makeQuery(id+"F1.opRevolve","SWEPT_BODY",BODY,{"disambiguationData":[OSD([sQuery(id+"F0.wireOp",EDGE,"E1")])]}),"instanceName":"1"}),"instanceName":"1"}),"instanceName":"1"}),"instanceName":"1"}),"instanceName":"1"}),"instanceName":"1"}),"instanceName":"1"}),"instanceName":"1"});
            var Q2765;
            Q2765=makeQuery(id+"F13.opPattern","COPY",BODY,{"derivedFrom":makeQuery(id+"F12.opPattern","COPY",BODY,{"derivedFrom":makeQuery(id+"F11.opPattern","COPY",BODY,{"derivedFrom":makeQuery(id+"F8.opPattern","COPY",BODY,{"derivedFrom":makeQuery(id+"F7.opPattern","COPY",BODY,{"derivedFrom":makeQuery(id+"F5.opPattern","COPY",BODY,{"derivedFrom":makeQuery(id+"F1.opRevolve","SWEPT_BODY",BODY,{"disambiguationData":[OSD([sQuery(id+"F0.wireOp",EDGE,"E1")])]}),"instanceName":"1"}),"instanceName":"1"}),"instanceName":"1"}),"instanceName":"1"}),"instanceName":"1"}),"instanceName":"1"});
            var Q2766;
            Q2766=makeQuery(id+"F13.opPattern","COPY",BODY,{"derivedFrom":makeQuery(id+"F12.opPattern","COPY",BODY,{"derivedFrom":makeQuery(id+"F11.opPattern","COPY",BODY,{"derivedFrom":makeQuery(id+"F8.opPattern","COPY",BODY,{"derivedFrom":makeQuery(id+"F7.opPattern","COPY",BODY,{"derivedFrom":makeQuery(id+"F5.opPattern","COPY",BODY,{"derivedFrom":makeQuery(id+"F2.opPattern","COPY",BODY,{"derivedFrom":makeQuery(id+"F1.opRevolve","SWEPT_BODY",BODY,{"disambiguationData":[OSD([sQuery(id+"F0.wireOp",EDGE,"E1")])]}),"instanceName":"1"}),"instanceName":"1"}),"instanceName":"1"}),"instanceName":"1"}),"instanceName":"1"}),"instanceName":"1"}),"instanceName":"1"});
            var Q2767;
            Q2767=makeQuery(id+"F13.opPattern","COPY",BODY,{"derivedFrom":makeQuery(id+"F12.opPattern","COPY",BODY,{"derivedFrom":makeQuery(id+"F11.opPattern","COPY",BODY,{"derivedFrom":makeQuery(id+"F8.opPattern","COPY",BODY,{"derivedFrom":makeQuery(id+"F7.opPattern","COPY",BODY,{"derivedFrom":makeQuery(id+"F5.opPattern","COPY",BODY,{"derivedFrom":makeQuery(id+"F3.opPattern","COPY",BODY,{"derivedFrom":makeQuery(id+"F2.opPattern","COPY",BODY,{"derivedFrom":makeQuery(id+"F1.opRevolve","SWEPT_BODY",BODY,{"disambiguationData":[OSD([sQuery(id+"F0.wireOp",EDGE,"E1")])]}),"instanceName":"1"}),"instanceName":"1"}),"instanceName":"1"}),"instanceName":"1"}),"instanceName":"1"}),"instanceName":"1"}),"instanceName":"1"}),"instanceName":"1"});
            var Q2768;
            Q2768=makeQuery(id+"F13.opPattern","COPY",BODY,{"derivedFrom":makeQuery(id+"F12.opPattern","COPY",BODY,{"derivedFrom":makeQuery(id+"F11.opPattern","COPY",BODY,{"derivedFrom":makeQuery(id+"F8.opPattern","COPY",BODY,{"derivedFrom":makeQuery(id+"F7.opPattern","COPY",BODY,{"derivedFrom":makeQuery(id+"F5.opPattern","COPY",BODY,{"derivedFrom":makeQuery(id+"F4.opPattern","COPY",BODY,{"derivedFrom":makeQuery(id+"F1.opRevolve","SWEPT_BODY",BODY,{"disambiguationData":[OSD([sQuery(id+"F0.wireOp",EDGE,"E1")])]}),"instanceName":"1"}),"instanceName":"1"}),"instanceName":"1"}),"instanceName":"1"}),"instanceName":"1"}),"instanceName":"1"}),"instanceName":"1"});
            var Q2769;
            Q2769=makeQuery(id+"F13.opPattern","COPY",BODY,{"derivedFrom":makeQuery(id+"F12.opPattern","COPY",BODY,{"derivedFrom":makeQuery(id+"F11.opPattern","COPY",BODY,{"derivedFrom":makeQuery(id+"F8.opPattern","COPY",BODY,{"derivedFrom":makeQuery(id+"F7.opPattern","COPY",BODY,{"derivedFrom":makeQuery(id+"F5.opPattern","COPY",BODY,{"derivedFrom":makeQuery(id+"F4.opPattern","COPY",BODY,{"derivedFrom":makeQuery(id+"F2.opPattern","COPY",BODY,{"derivedFrom":makeQuery(id+"F1.opRevolve","SWEPT_BODY",BODY,{"disambiguationData":[OSD([sQuery(id+"F0.wireOp",EDGE,"E1")])]}),"instanceName":"1"}),"instanceName":"1"}),"instanceName":"1"}),"instanceName":"1"}),"instanceName":"1"}),"instanceName":"1"}),"instanceName":"1"}),"instanceName":"1"});
            var Q2770;
            Q2770=makeQuery(id+"F13.opPattern","COPY",BODY,{"derivedFrom":makeQuery(id+"F12.opPattern","COPY",BODY,{"derivedFrom":makeQuery(id+"F11.opPattern","COPY",BODY,{"derivedFrom":makeQuery(id+"F8.opPattern","COPY",BODY,{"derivedFrom":makeQuery(id+"F7.opPattern","COPY",BODY,{"derivedFrom":makeQuery(id+"F5.opPattern","COPY",BODY,{"derivedFrom":makeQuery(id+"F4.opPattern","COPY",BODY,{"derivedFrom":makeQuery(id+"F3.opPattern","COPY",BODY,{"derivedFrom":makeQuery(id+"F2.opPattern","COPY",BODY,{"derivedFrom":makeQuery(id+"F1.opRevolve","SWEPT_BODY",BODY,{"disambiguationData":[OSD([sQuery(id+"F0.wireOp",EDGE,"E1")])]}),"instanceName":"1"}),"instanceName":"1"}),"instanceName":"1"}),"instanceName":"1"}),"instanceName":"1"}),"instanceName":"1"}),"instanceName":"1"}),"instanceName":"1"}),"instanceName":"1"});
            var Q2771;
            Q2771=makeQuery(id+"F13.opPattern","COPY",BODY,{"derivedFrom":makeQuery(id+"F12.opPattern","COPY",BODY,{"derivedFrom":makeQuery(id+"F11.opPattern","COPY",BODY,{"derivedFrom":makeQuery(id+"F8.opPattern","COPY",BODY,{"derivedFrom":makeQuery(id+"F7.opPattern","COPY",BODY,{"derivedFrom":makeQuery(id+"F6.opPattern","COPY",BODY,{"derivedFrom":makeQuery(id+"F1.opRevolve","SWEPT_BODY",BODY,{"disambiguationData":[OSD([sQuery(id+"F0.wireOp",EDGE,"E1")])]}),"instanceName":"1"}),"instanceName":"1"}),"instanceName":"1"}),"instanceName":"1"}),"instanceName":"1"}),"instanceName":"1"});
            var Q2772;
            Q2772=makeQuery(id+"F13.opPattern","COPY",BODY,{"derivedFrom":makeQuery(id+"F12.opPattern","COPY",BODY,{"derivedFrom":makeQuery(id+"F11.opPattern","COPY",BODY,{"derivedFrom":makeQuery(id+"F8.opPattern","COPY",BODY,{"derivedFrom":makeQuery(id+"F7.opPattern","COPY",BODY,{"derivedFrom":makeQuery(id+"F6.opPattern","COPY",BODY,{"derivedFrom":makeQuery(id+"F2.opPattern","COPY",BODY,{"derivedFrom":makeQuery(id+"F1.opRevolve","SWEPT_BODY",BODY,{"disambiguationData":[OSD([sQuery(id+"F0.wireOp",EDGE,"E1")])]}),"instanceName":"1"}),"instanceName":"1"}),"instanceName":"1"}),"instanceName":"1"}),"instanceName":"1"}),"instanceName":"1"}),"instanceName":"1"});
            var Q2773;
            Q2773=makeQuery(id+"F13.opPattern","COPY",BODY,{"derivedFrom":makeQuery(id+"F12.opPattern","COPY",BODY,{"derivedFrom":makeQuery(id+"F11.opPattern","COPY",BODY,{"derivedFrom":makeQuery(id+"F8.opPattern","COPY",BODY,{"derivedFrom":makeQuery(id+"F7.opPattern","COPY",BODY,{"derivedFrom":makeQuery(id+"F6.opPattern","COPY",BODY,{"derivedFrom":makeQuery(id+"F3.opPattern","COPY",BODY,{"derivedFrom":makeQuery(id+"F2.opPattern","COPY",BODY,{"derivedFrom":makeQuery(id+"F1.opRevolve","SWEPT_BODY",BODY,{"disambiguationData":[OSD([sQuery(id+"F0.wireOp",EDGE,"E1")])]}),"instanceName":"1"}),"instanceName":"1"}),"instanceName":"1"}),"instanceName":"1"}),"instanceName":"1"}),"instanceName":"1"}),"instanceName":"1"}),"instanceName":"1"});
            var Q2774;
            Q2774=makeQuery(id+"F13.opPattern","COPY",BODY,{"derivedFrom":makeQuery(id+"F12.opPattern","COPY",BODY,{"derivedFrom":makeQuery(id+"F11.opPattern","COPY",BODY,{"derivedFrom":makeQuery(id+"F8.opPattern","COPY",BODY,{"derivedFrom":makeQuery(id+"F7.opPattern","COPY",BODY,{"derivedFrom":makeQuery(id+"F6.opPattern","COPY",BODY,{"derivedFrom":makeQuery(id+"F4.opPattern","COPY",BODY,{"derivedFrom":makeQuery(id+"F1.opRevolve","SWEPT_BODY",BODY,{"disambiguationData":[OSD([sQuery(id+"F0.wireOp",EDGE,"E1")])]}),"instanceName":"1"}),"instanceName":"1"}),"instanceName":"1"}),"instanceName":"1"}),"instanceName":"1"}),"instanceName":"1"}),"instanceName":"1"});
            var Q2775;
            Q2775=makeQuery(id+"F13.opPattern","COPY",BODY,{"derivedFrom":makeQuery(id+"F12.opPattern","COPY",BODY,{"derivedFrom":makeQuery(id+"F11.opPattern","COPY",BODY,{"derivedFrom":makeQuery(id+"F8.opPattern","COPY",BODY,{"derivedFrom":makeQuery(id+"F7.opPattern","COPY",BODY,{"derivedFrom":makeQuery(id+"F6.opPattern","COPY",BODY,{"derivedFrom":makeQuery(id+"F4.opPattern","COPY",BODY,{"derivedFrom":makeQuery(id+"F2.opPattern","COPY",BODY,{"derivedFrom":makeQuery(id+"F1.opRevolve","SWEPT_BODY",BODY,{"disambiguationData":[OSD([sQuery(id+"F0.wireOp",EDGE,"E1")])]}),"instanceName":"1"}),"instanceName":"1"}),"instanceName":"1"}),"instanceName":"1"}),"instanceName":"1"}),"instanceName":"1"}),"instanceName":"1"}),"instanceName":"1"});
            var Q2776;
            Q2776=makeQuery(id+"F13.opPattern","COPY",BODY,{"derivedFrom":makeQuery(id+"F12.opPattern","COPY",BODY,{"derivedFrom":makeQuery(id+"F11.opPattern","COPY",BODY,{"derivedFrom":makeQuery(id+"F8.opPattern","COPY",BODY,{"derivedFrom":makeQuery(id+"F7.opPattern","COPY",BODY,{"derivedFrom":makeQuery(id+"F6.opPattern","COPY",BODY,{"derivedFrom":makeQuery(id+"F4.opPattern","COPY",BODY,{"derivedFrom":makeQuery(id+"F3.opPattern","COPY",BODY,{"derivedFrom":makeQuery(id+"F2.opPattern","COPY",BODY,{"derivedFrom":makeQuery(id+"F1.opRevolve","SWEPT_BODY",BODY,{"disambiguationData":[OSD([sQuery(id+"F0.wireOp",EDGE,"E1")])]}),"instanceName":"1"}),"instanceName":"1"}),"instanceName":"1"}),"instanceName":"1"}),"instanceName":"1"}),"instanceName":"1"}),"instanceName":"1"}),"instanceName":"1"}),"instanceName":"1"});
            var Q2777;
            Q2777=makeQuery(id+"F13.opPattern","COPY",BODY,{"derivedFrom":makeQuery(id+"F12.opPattern","COPY",BODY,{"derivedFrom":makeQuery(id+"F11.opPattern","COPY",BODY,{"derivedFrom":makeQuery(id+"F8.opPattern","COPY",BODY,{"derivedFrom":makeQuery(id+"F7.opPattern","COPY",BODY,{"derivedFrom":makeQuery(id+"F6.opPattern","COPY",BODY,{"derivedFrom":makeQuery(id+"F5.opPattern","COPY",BODY,{"derivedFrom":makeQuery(id+"F1.opRevolve","SWEPT_BODY",BODY,{"disambiguationData":[OSD([sQuery(id+"F0.wireOp",EDGE,"E1")])]}),"instanceName":"1"}),"instanceName":"1"}),"instanceName":"1"}),"instanceName":"1"}),"instanceName":"1"}),"instanceName":"1"}),"instanceName":"1"});
            var Q2778;
            Q2778=makeQuery(id+"F13.opPattern","COPY",BODY,{"derivedFrom":makeQuery(id+"F12.opPattern","COPY",BODY,{"derivedFrom":makeQuery(id+"F11.opPattern","COPY",BODY,{"derivedFrom":makeQuery(id+"F8.opPattern","COPY",BODY,{"derivedFrom":makeQuery(id+"F7.opPattern","COPY",BODY,{"derivedFrom":makeQuery(id+"F6.opPattern","COPY",BODY,{"derivedFrom":makeQuery(id+"F5.opPattern","COPY",BODY,{"derivedFrom":makeQuery(id+"F2.opPattern","COPY",BODY,{"derivedFrom":makeQuery(id+"F1.opRevolve","SWEPT_BODY",BODY,{"disambiguationData":[OSD([sQuery(id+"F0.wireOp",EDGE,"E1")])]}),"instanceName":"1"}),"instanceName":"1"}),"instanceName":"1"}),"instanceName":"1"}),"instanceName":"1"}),"instanceName":"1"}),"instanceName":"1"}),"instanceName":"1"});
            var Q2779;
            Q2779=makeQuery(id+"F13.opPattern","COPY",BODY,{"derivedFrom":makeQuery(id+"F12.opPattern","COPY",BODY,{"derivedFrom":makeQuery(id+"F11.opPattern","COPY",BODY,{"derivedFrom":makeQuery(id+"F8.opPattern","COPY",BODY,{"derivedFrom":makeQuery(id+"F7.opPattern","COPY",BODY,{"derivedFrom":makeQuery(id+"F6.opPattern","COPY",BODY,{"derivedFrom":makeQuery(id+"F5.opPattern","COPY",BODY,{"derivedFrom":makeQuery(id+"F3.opPattern","COPY",BODY,{"derivedFrom":makeQuery(id+"F2.opPattern","COPY",BODY,{"derivedFrom":makeQuery(id+"F1.opRevolve","SWEPT_BODY",BODY,{"disambiguationData":[OSD([sQuery(id+"F0.wireOp",EDGE,"E1")])]}),"instanceName":"1"}),"instanceName":"1"}),"instanceName":"1"}),"instanceName":"1"}),"instanceName":"1"}),"instanceName":"1"}),"instanceName":"1"}),"instanceName":"1"}),"instanceName":"1"});
            var Q2780;
            Q2780=makeQuery(id+"F13.opPattern","COPY",BODY,{"derivedFrom":makeQuery(id+"F12.opPattern","COPY",BODY,{"derivedFrom":makeQuery(id+"F11.opPattern","COPY",BODY,{"derivedFrom":makeQuery(id+"F8.opPattern","COPY",BODY,{"derivedFrom":makeQuery(id+"F7.opPattern","COPY",BODY,{"derivedFrom":makeQuery(id+"F6.opPattern","COPY",BODY,{"derivedFrom":makeQuery(id+"F5.opPattern","COPY",BODY,{"derivedFrom":makeQuery(id+"F4.opPattern","COPY",BODY,{"derivedFrom":makeQuery(id+"F1.opRevolve","SWEPT_BODY",BODY,{"disambiguationData":[OSD([sQuery(id+"F0.wireOp",EDGE,"E1")])]}),"instanceName":"1"}),"instanceName":"1"}),"instanceName":"1"}),"instanceName":"1"}),"instanceName":"1"}),"instanceName":"1"}),"instanceName":"1"}),"instanceName":"1"});
            var Q2781;
            Q2781=makeQuery(id+"F13.opPattern","COPY",BODY,{"derivedFrom":makeQuery(id+"F12.opPattern","COPY",BODY,{"derivedFrom":makeQuery(id+"F11.opPattern","COPY",BODY,{"derivedFrom":makeQuery(id+"F8.opPattern","COPY",BODY,{"derivedFrom":makeQuery(id+"F7.opPattern","COPY",BODY,{"derivedFrom":makeQuery(id+"F6.opPattern","COPY",BODY,{"derivedFrom":makeQuery(id+"F5.opPattern","COPY",BODY,{"derivedFrom":makeQuery(id+"F4.opPattern","COPY",BODY,{"derivedFrom":makeQuery(id+"F2.opPattern","COPY",BODY,{"derivedFrom":makeQuery(id+"F1.opRevolve","SWEPT_BODY",BODY,{"disambiguationData":[OSD([sQuery(id+"F0.wireOp",EDGE,"E1")])]}),"instanceName":"1"}),"instanceName":"1"}),"instanceName":"1"}),"instanceName":"1"}),"instanceName":"1"}),"instanceName":"1"}),"instanceName":"1"}),"instanceName":"1"}),"instanceName":"1"});
            var Q2782;
            Q2782=makeQuery(id+"F13.opPattern","COPY",BODY,{"derivedFrom":makeQuery(id+"F12.opPattern","COPY",BODY,{"derivedFrom":makeQuery(id+"F11.opPattern","COPY",BODY,{"derivedFrom":makeQuery(id+"F8.opPattern","COPY",BODY,{"derivedFrom":makeQuery(id+"F7.opPattern","COPY",BODY,{"derivedFrom":makeQuery(id+"F6.opPattern","COPY",BODY,{"derivedFrom":makeQuery(id+"F5.opPattern","COPY",BODY,{"derivedFrom":makeQuery(id+"F4.opPattern","COPY",BODY,{"derivedFrom":makeQuery(id+"F3.opPattern","COPY",BODY,{"derivedFrom":makeQuery(id+"F2.opPattern","COPY",BODY,{"derivedFrom":makeQuery(id+"F1.opRevolve","SWEPT_BODY",BODY,{"disambiguationData":[OSD([sQuery(id+"F0.wireOp",EDGE,"E1")])]}),"instanceName":"1"}),"instanceName":"1"}),"instanceName":"1"}),"instanceName":"1"}),"instanceName":"1"}),"instanceName":"1"}),"instanceName":"1"}),"instanceName":"1"}),"instanceName":"1"}),"instanceName":"1"});
            var Q2783;
            Q2783=makeQuery(id+"F13.opPattern","COPY",BODY,{"derivedFrom":makeQuery(id+"F12.opPattern","COPY",BODY,{"derivedFrom":makeQuery(id+"F11.opPattern","COPY",BODY,{"derivedFrom":makeQuery(id+"F9.opPattern","COPY",BODY,{"derivedFrom":makeQuery(id+"F1.opRevolve","SWEPT_BODY",BODY,{"disambiguationData":[OSD([sQuery(id+"F0.wireOp",EDGE,"E1")])]}),"instanceName":"1"}),"instanceName":"1"}),"instanceName":"1"}),"instanceName":"1"});
            var Q2784;
            Q2784=makeQuery(id+"F13.opPattern","COPY",BODY,{"derivedFrom":makeQuery(id+"F12.opPattern","COPY",BODY,{"derivedFrom":makeQuery(id+"F11.opPattern","COPY",BODY,{"derivedFrom":makeQuery(id+"F9.opPattern","COPY",BODY,{"derivedFrom":makeQuery(id+"F2.opPattern","COPY",BODY,{"derivedFrom":makeQuery(id+"F1.opRevolve","SWEPT_BODY",BODY,{"disambiguationData":[OSD([sQuery(id+"F0.wireOp",EDGE,"E1")])]}),"instanceName":"1"}),"instanceName":"1"}),"instanceName":"1"}),"instanceName":"1"}),"instanceName":"1"});
            var Q2785;
            Q2785=makeQuery(id+"F13.opPattern","COPY",BODY,{"derivedFrom":makeQuery(id+"F12.opPattern","COPY",BODY,{"derivedFrom":makeQuery(id+"F11.opPattern","COPY",BODY,{"derivedFrom":makeQuery(id+"F9.opPattern","COPY",BODY,{"derivedFrom":makeQuery(id+"F3.opPattern","COPY",BODY,{"derivedFrom":makeQuery(id+"F2.opPattern","COPY",BODY,{"derivedFrom":makeQuery(id+"F1.opRevolve","SWEPT_BODY",BODY,{"disambiguationData":[OSD([sQuery(id+"F0.wireOp",EDGE,"E1")])]}),"instanceName":"1"}),"instanceName":"1"}),"instanceName":"1"}),"instanceName":"1"}),"instanceName":"1"}),"instanceName":"1"});
            var Q2786;
            Q2786=makeQuery(id+"F13.opPattern","COPY",BODY,{"derivedFrom":makeQuery(id+"F12.opPattern","COPY",BODY,{"derivedFrom":makeQuery(id+"F11.opPattern","COPY",BODY,{"derivedFrom":makeQuery(id+"F9.opPattern","COPY",BODY,{"derivedFrom":makeQuery(id+"F4.opPattern","COPY",BODY,{"derivedFrom":makeQuery(id+"F1.opRevolve","SWEPT_BODY",BODY,{"disambiguationData":[OSD([sQuery(id+"F0.wireOp",EDGE,"E1")])]}),"instanceName":"1"}),"instanceName":"1"}),"instanceName":"1"}),"instanceName":"1"}),"instanceName":"1"});
            var Q2787;
            Q2787=makeQuery(id+"F13.opPattern","COPY",BODY,{"derivedFrom":makeQuery(id+"F12.opPattern","COPY",BODY,{"derivedFrom":makeQuery(id+"F11.opPattern","COPY",BODY,{"derivedFrom":makeQuery(id+"F9.opPattern","COPY",BODY,{"derivedFrom":makeQuery(id+"F4.opPattern","COPY",BODY,{"derivedFrom":makeQuery(id+"F2.opPattern","COPY",BODY,{"derivedFrom":makeQuery(id+"F1.opRevolve","SWEPT_BODY",BODY,{"disambiguationData":[OSD([sQuery(id+"F0.wireOp",EDGE,"E1")])]}),"instanceName":"1"}),"instanceName":"1"}),"instanceName":"1"}),"instanceName":"1"}),"instanceName":"1"}),"instanceName":"1"});
            var Q2788;
            Q2788=makeQuery(id+"F13.opPattern","COPY",BODY,{"derivedFrom":makeQuery(id+"F12.opPattern","COPY",BODY,{"derivedFrom":makeQuery(id+"F11.opPattern","COPY",BODY,{"derivedFrom":makeQuery(id+"F9.opPattern","COPY",BODY,{"derivedFrom":makeQuery(id+"F4.opPattern","COPY",BODY,{"derivedFrom":makeQuery(id+"F3.opPattern","COPY",BODY,{"derivedFrom":makeQuery(id+"F2.opPattern","COPY",BODY,{"derivedFrom":makeQuery(id+"F1.opRevolve","SWEPT_BODY",BODY,{"disambiguationData":[OSD([sQuery(id+"F0.wireOp",EDGE,"E1")])]}),"instanceName":"1"}),"instanceName":"1"}),"instanceName":"1"}),"instanceName":"1"}),"instanceName":"1"}),"instanceName":"1"}),"instanceName":"1"});
            var Q2789;
            Q2789=makeQuery(id+"F13.opPattern","COPY",BODY,{"derivedFrom":makeQuery(id+"F12.opPattern","COPY",BODY,{"derivedFrom":makeQuery(id+"F11.opPattern","COPY",BODY,{"derivedFrom":makeQuery(id+"F9.opPattern","COPY",BODY,{"derivedFrom":makeQuery(id+"F5.opPattern","COPY",BODY,{"derivedFrom":makeQuery(id+"F1.opRevolve","SWEPT_BODY",BODY,{"disambiguationData":[OSD([sQuery(id+"F0.wireOp",EDGE,"E1")])]}),"instanceName":"1"}),"instanceName":"1"}),"instanceName":"1"}),"instanceName":"1"}),"instanceName":"1"});
            var Q2790;
            Q2790=makeQuery(id+"F13.opPattern","COPY",BODY,{"derivedFrom":makeQuery(id+"F12.opPattern","COPY",BODY,{"derivedFrom":makeQuery(id+"F11.opPattern","COPY",BODY,{"derivedFrom":makeQuery(id+"F9.opPattern","COPY",BODY,{"derivedFrom":makeQuery(id+"F5.opPattern","COPY",BODY,{"derivedFrom":makeQuery(id+"F2.opPattern","COPY",BODY,{"derivedFrom":makeQuery(id+"F1.opRevolve","SWEPT_BODY",BODY,{"disambiguationData":[OSD([sQuery(id+"F0.wireOp",EDGE,"E1")])]}),"instanceName":"1"}),"instanceName":"1"}),"instanceName":"1"}),"instanceName":"1"}),"instanceName":"1"}),"instanceName":"1"});
            var Q2791;
            Q2791=makeQuery(id+"F13.opPattern","COPY",BODY,{"derivedFrom":makeQuery(id+"F12.opPattern","COPY",BODY,{"derivedFrom":makeQuery(id+"F11.opPattern","COPY",BODY,{"derivedFrom":makeQuery(id+"F9.opPattern","COPY",BODY,{"derivedFrom":makeQuery(id+"F5.opPattern","COPY",BODY,{"derivedFrom":makeQuery(id+"F3.opPattern","COPY",BODY,{"derivedFrom":makeQuery(id+"F2.opPattern","COPY",BODY,{"derivedFrom":makeQuery(id+"F1.opRevolve","SWEPT_BODY",BODY,{"disambiguationData":[OSD([sQuery(id+"F0.wireOp",EDGE,"E1")])]}),"instanceName":"1"}),"instanceName":"1"}),"instanceName":"1"}),"instanceName":"1"}),"instanceName":"1"}),"instanceName":"1"}),"instanceName":"1"});
            var Q2792;
            Q2792=makeQuery(id+"F13.opPattern","COPY",BODY,{"derivedFrom":makeQuery(id+"F12.opPattern","COPY",BODY,{"derivedFrom":makeQuery(id+"F11.opPattern","COPY",BODY,{"derivedFrom":makeQuery(id+"F9.opPattern","COPY",BODY,{"derivedFrom":makeQuery(id+"F5.opPattern","COPY",BODY,{"derivedFrom":makeQuery(id+"F4.opPattern","COPY",BODY,{"derivedFrom":makeQuery(id+"F1.opRevolve","SWEPT_BODY",BODY,{"disambiguationData":[OSD([sQuery(id+"F0.wireOp",EDGE,"E1")])]}),"instanceName":"1"}),"instanceName":"1"}),"instanceName":"1"}),"instanceName":"1"}),"instanceName":"1"}),"instanceName":"1"});
            var Q2793;
            Q2793=makeQuery(id+"F13.opPattern","COPY",BODY,{"derivedFrom":makeQuery(id+"F12.opPattern","COPY",BODY,{"derivedFrom":makeQuery(id+"F11.opPattern","COPY",BODY,{"derivedFrom":makeQuery(id+"F9.opPattern","COPY",BODY,{"derivedFrom":makeQuery(id+"F5.opPattern","COPY",BODY,{"derivedFrom":makeQuery(id+"F4.opPattern","COPY",BODY,{"derivedFrom":makeQuery(id+"F2.opPattern","COPY",BODY,{"derivedFrom":makeQuery(id+"F1.opRevolve","SWEPT_BODY",BODY,{"disambiguationData":[OSD([sQuery(id+"F0.wireOp",EDGE,"E1")])]}),"instanceName":"1"}),"instanceName":"1"}),"instanceName":"1"}),"instanceName":"1"}),"instanceName":"1"}),"instanceName":"1"}),"instanceName":"1"});
            var Q2794;
            Q2794=makeQuery(id+"F13.opPattern","COPY",BODY,{"derivedFrom":makeQuery(id+"F12.opPattern","COPY",BODY,{"derivedFrom":makeQuery(id+"F11.opPattern","COPY",BODY,{"derivedFrom":makeQuery(id+"F9.opPattern","COPY",BODY,{"derivedFrom":makeQuery(id+"F5.opPattern","COPY",BODY,{"derivedFrom":makeQuery(id+"F4.opPattern","COPY",BODY,{"derivedFrom":makeQuery(id+"F3.opPattern","COPY",BODY,{"derivedFrom":makeQuery(id+"F2.opPattern","COPY",BODY,{"derivedFrom":makeQuery(id+"F1.opRevolve","SWEPT_BODY",BODY,{"disambiguationData":[OSD([sQuery(id+"F0.wireOp",EDGE,"E1")])]}),"instanceName":"1"}),"instanceName":"1"}),"instanceName":"1"}),"instanceName":"1"}),"instanceName":"1"}),"instanceName":"1"}),"instanceName":"1"}),"instanceName":"1"});
            var Q2795;
            Q2795=makeQuery(id+"F13.opPattern","COPY",BODY,{"derivedFrom":makeQuery(id+"F12.opPattern","COPY",BODY,{"derivedFrom":makeQuery(id+"F11.opPattern","COPY",BODY,{"derivedFrom":makeQuery(id+"F9.opPattern","COPY",BODY,{"derivedFrom":makeQuery(id+"F6.opPattern","COPY",BODY,{"derivedFrom":makeQuery(id+"F1.opRevolve","SWEPT_BODY",BODY,{"disambiguationData":[OSD([sQuery(id+"F0.wireOp",EDGE,"E1")])]}),"instanceName":"1"}),"instanceName":"1"}),"instanceName":"1"}),"instanceName":"1"}),"instanceName":"1"});
            var Q2796;
            Q2796=makeQuery(id+"F13.opPattern","COPY",BODY,{"derivedFrom":makeQuery(id+"F12.opPattern","COPY",BODY,{"derivedFrom":makeQuery(id+"F11.opPattern","COPY",BODY,{"derivedFrom":makeQuery(id+"F9.opPattern","COPY",BODY,{"derivedFrom":makeQuery(id+"F6.opPattern","COPY",BODY,{"derivedFrom":makeQuery(id+"F2.opPattern","COPY",BODY,{"derivedFrom":makeQuery(id+"F1.opRevolve","SWEPT_BODY",BODY,{"disambiguationData":[OSD([sQuery(id+"F0.wireOp",EDGE,"E1")])]}),"instanceName":"1"}),"instanceName":"1"}),"instanceName":"1"}),"instanceName":"1"}),"instanceName":"1"}),"instanceName":"1"});
            var Q2797;
            Q2797=makeQuery(id+"F13.opPattern","COPY",BODY,{"derivedFrom":makeQuery(id+"F12.opPattern","COPY",BODY,{"derivedFrom":makeQuery(id+"F11.opPattern","COPY",BODY,{"derivedFrom":makeQuery(id+"F9.opPattern","COPY",BODY,{"derivedFrom":makeQuery(id+"F6.opPattern","COPY",BODY,{"derivedFrom":makeQuery(id+"F3.opPattern","COPY",BODY,{"derivedFrom":makeQuery(id+"F2.opPattern","COPY",BODY,{"derivedFrom":makeQuery(id+"F1.opRevolve","SWEPT_BODY",BODY,{"disambiguationData":[OSD([sQuery(id+"F0.wireOp",EDGE,"E1")])]}),"instanceName":"1"}),"instanceName":"1"}),"instanceName":"1"}),"instanceName":"1"}),"instanceName":"1"}),"instanceName":"1"}),"instanceName":"1"});
            var Q2798;
            Q2798=makeQuery(id+"F13.opPattern","COPY",BODY,{"derivedFrom":makeQuery(id+"F12.opPattern","COPY",BODY,{"derivedFrom":makeQuery(id+"F11.opPattern","COPY",BODY,{"derivedFrom":makeQuery(id+"F9.opPattern","COPY",BODY,{"derivedFrom":makeQuery(id+"F6.opPattern","COPY",BODY,{"derivedFrom":makeQuery(id+"F4.opPattern","COPY",BODY,{"derivedFrom":makeQuery(id+"F1.opRevolve","SWEPT_BODY",BODY,{"disambiguationData":[OSD([sQuery(id+"F0.wireOp",EDGE,"E1")])]}),"instanceName":"1"}),"instanceName":"1"}),"instanceName":"1"}),"instanceName":"1"}),"instanceName":"1"}),"instanceName":"1"});
            var Q2799;
            Q2799=makeQuery(id+"F13.opPattern","COPY",BODY,{"derivedFrom":makeQuery(id+"F12.opPattern","COPY",BODY,{"derivedFrom":makeQuery(id+"F11.opPattern","COPY",BODY,{"derivedFrom":makeQuery(id+"F9.opPattern","COPY",BODY,{"derivedFrom":makeQuery(id+"F6.opPattern","COPY",BODY,{"derivedFrom":makeQuery(id+"F4.opPattern","COPY",BODY,{"derivedFrom":makeQuery(id+"F2.opPattern","COPY",BODY,{"derivedFrom":makeQuery(id+"F1.opRevolve","SWEPT_BODY",BODY,{"disambiguationData":[OSD([sQuery(id+"F0.wireOp",EDGE,"E1")])]}),"instanceName":"1"}),"instanceName":"1"}),"instanceName":"1"}),"instanceName":"1"}),"instanceName":"1"}),"instanceName":"1"}),"instanceName":"1"});
            var Q2800;
            Q2800=makeQuery(id+"F13.opPattern","COPY",BODY,{"derivedFrom":makeQuery(id+"F12.opPattern","COPY",BODY,{"derivedFrom":makeQuery(id+"F11.opPattern","COPY",BODY,{"derivedFrom":makeQuery(id+"F9.opPattern","COPY",BODY,{"derivedFrom":makeQuery(id+"F6.opPattern","COPY",BODY,{"derivedFrom":makeQuery(id+"F4.opPattern","COPY",BODY,{"derivedFrom":makeQuery(id+"F3.opPattern","COPY",BODY,{"derivedFrom":makeQuery(id+"F2.opPattern","COPY",BODY,{"derivedFrom":makeQuery(id+"F1.opRevolve","SWEPT_BODY",BODY,{"disambiguationData":[OSD([sQuery(id+"F0.wireOp",EDGE,"E1")])]}),"instanceName":"1"}),"instanceName":"1"}),"instanceName":"1"}),"instanceName":"1"}),"instanceName":"1"}),"instanceName":"1"}),"instanceName":"1"}),"instanceName":"1"});
            var Q2801;
            Q2801=makeQuery(id+"F13.opPattern","COPY",BODY,{"derivedFrom":makeQuery(id+"F12.opPattern","COPY",BODY,{"derivedFrom":makeQuery(id+"F11.opPattern","COPY",BODY,{"derivedFrom":makeQuery(id+"F9.opPattern","COPY",BODY,{"derivedFrom":makeQuery(id+"F6.opPattern","COPY",BODY,{"derivedFrom":makeQuery(id+"F5.opPattern","COPY",BODY,{"derivedFrom":makeQuery(id+"F1.opRevolve","SWEPT_BODY",BODY,{"disambiguationData":[OSD([sQuery(id+"F0.wireOp",EDGE,"E1")])]}),"instanceName":"1"}),"instanceName":"1"}),"instanceName":"1"}),"instanceName":"1"}),"instanceName":"1"}),"instanceName":"1"});
            var Q2802;
            Q2802=makeQuery(id+"F13.opPattern","COPY",BODY,{"derivedFrom":makeQuery(id+"F12.opPattern","COPY",BODY,{"derivedFrom":makeQuery(id+"F11.opPattern","COPY",BODY,{"derivedFrom":makeQuery(id+"F9.opPattern","COPY",BODY,{"derivedFrom":makeQuery(id+"F6.opPattern","COPY",BODY,{"derivedFrom":makeQuery(id+"F5.opPattern","COPY",BODY,{"derivedFrom":makeQuery(id+"F2.opPattern","COPY",BODY,{"derivedFrom":makeQuery(id+"F1.opRevolve","SWEPT_BODY",BODY,{"disambiguationData":[OSD([sQuery(id+"F0.wireOp",EDGE,"E1")])]}),"instanceName":"1"}),"instanceName":"1"}),"instanceName":"1"}),"instanceName":"1"}),"instanceName":"1"}),"instanceName":"1"}),"instanceName":"1"});
            var Q2803;
            Q2803=makeQuery(id+"F13.opPattern","COPY",BODY,{"derivedFrom":makeQuery(id+"F12.opPattern","COPY",BODY,{"derivedFrom":makeQuery(id+"F11.opPattern","COPY",BODY,{"derivedFrom":makeQuery(id+"F9.opPattern","COPY",BODY,{"derivedFrom":makeQuery(id+"F6.opPattern","COPY",BODY,{"derivedFrom":makeQuery(id+"F5.opPattern","COPY",BODY,{"derivedFrom":makeQuery(id+"F3.opPattern","COPY",BODY,{"derivedFrom":makeQuery(id+"F2.opPattern","COPY",BODY,{"derivedFrom":makeQuery(id+"F1.opRevolve","SWEPT_BODY",BODY,{"disambiguationData":[OSD([sQuery(id+"F0.wireOp",EDGE,"E1")])]}),"instanceName":"1"}),"instanceName":"1"}),"instanceName":"1"}),"instanceName":"1"}),"instanceName":"1"}),"instanceName":"1"}),"instanceName":"1"}),"instanceName":"1"});
            var Q2804;
            Q2804=makeQuery(id+"F13.opPattern","COPY",BODY,{"derivedFrom":makeQuery(id+"F12.opPattern","COPY",BODY,{"derivedFrom":makeQuery(id+"F11.opPattern","COPY",BODY,{"derivedFrom":makeQuery(id+"F9.opPattern","COPY",BODY,{"derivedFrom":makeQuery(id+"F6.opPattern","COPY",BODY,{"derivedFrom":makeQuery(id+"F5.opPattern","COPY",BODY,{"derivedFrom":makeQuery(id+"F4.opPattern","COPY",BODY,{"derivedFrom":makeQuery(id+"F1.opRevolve","SWEPT_BODY",BODY,{"disambiguationData":[OSD([sQuery(id+"F0.wireOp",EDGE,"E1")])]}),"instanceName":"1"}),"instanceName":"1"}),"instanceName":"1"}),"instanceName":"1"}),"instanceName":"1"}),"instanceName":"1"}),"instanceName":"1"});
            var Q2805;
            Q2805=makeQuery(id+"F13.opPattern","COPY",BODY,{"derivedFrom":makeQuery(id+"F12.opPattern","COPY",BODY,{"derivedFrom":makeQuery(id+"F11.opPattern","COPY",BODY,{"derivedFrom":makeQuery(id+"F9.opPattern","COPY",BODY,{"derivedFrom":makeQuery(id+"F6.opPattern","COPY",BODY,{"derivedFrom":makeQuery(id+"F5.opPattern","COPY",BODY,{"derivedFrom":makeQuery(id+"F4.opPattern","COPY",BODY,{"derivedFrom":makeQuery(id+"F2.opPattern","COPY",BODY,{"derivedFrom":makeQuery(id+"F1.opRevolve","SWEPT_BODY",BODY,{"disambiguationData":[OSD([sQuery(id+"F0.wireOp",EDGE,"E1")])]}),"instanceName":"1"}),"instanceName":"1"}),"instanceName":"1"}),"instanceName":"1"}),"instanceName":"1"}),"instanceName":"1"}),"instanceName":"1"}),"instanceName":"1"});
            var Q2806;
            Q2806=makeQuery(id+"F13.opPattern","COPY",BODY,{"derivedFrom":makeQuery(id+"F12.opPattern","COPY",BODY,{"derivedFrom":makeQuery(id+"F11.opPattern","COPY",BODY,{"derivedFrom":makeQuery(id+"F9.opPattern","COPY",BODY,{"derivedFrom":makeQuery(id+"F6.opPattern","COPY",BODY,{"derivedFrom":makeQuery(id+"F5.opPattern","COPY",BODY,{"derivedFrom":makeQuery(id+"F4.opPattern","COPY",BODY,{"derivedFrom":makeQuery(id+"F3.opPattern","COPY",BODY,{"derivedFrom":makeQuery(id+"F2.opPattern","COPY",BODY,{"derivedFrom":makeQuery(id+"F1.opRevolve","SWEPT_BODY",BODY,{"disambiguationData":[OSD([sQuery(id+"F0.wireOp",EDGE,"E1")])]}),"instanceName":"1"}),"instanceName":"1"}),"instanceName":"1"}),"instanceName":"1"}),"instanceName":"1"}),"instanceName":"1"}),"instanceName":"1"}),"instanceName":"1"}),"instanceName":"1"});
            var Q2807;
            Q2807=makeQuery(id+"F13.opPattern","COPY",BODY,{"derivedFrom":makeQuery(id+"F12.opPattern","COPY",BODY,{"derivedFrom":makeQuery(id+"F11.opPattern","COPY",BODY,{"derivedFrom":makeQuery(id+"F9.opPattern","COPY",BODY,{"derivedFrom":makeQuery(id+"F7.opPattern","COPY",BODY,{"derivedFrom":makeQuery(id+"F1.opRevolve","SWEPT_BODY",BODY,{"disambiguationData":[OSD([sQuery(id+"F0.wireOp",EDGE,"E1")])]}),"instanceName":"1"}),"instanceName":"1"}),"instanceName":"1"}),"instanceName":"1"}),"instanceName":"1"});
            var Q2808;
            Q2808=makeQuery(id+"F13.opPattern","COPY",BODY,{"derivedFrom":makeQuery(id+"F12.opPattern","COPY",BODY,{"derivedFrom":makeQuery(id+"F11.opPattern","COPY",BODY,{"derivedFrom":makeQuery(id+"F9.opPattern","COPY",BODY,{"derivedFrom":makeQuery(id+"F7.opPattern","COPY",BODY,{"derivedFrom":makeQuery(id+"F2.opPattern","COPY",BODY,{"derivedFrom":makeQuery(id+"F1.opRevolve","SWEPT_BODY",BODY,{"disambiguationData":[OSD([sQuery(id+"F0.wireOp",EDGE,"E1")])]}),"instanceName":"1"}),"instanceName":"1"}),"instanceName":"1"}),"instanceName":"1"}),"instanceName":"1"}),"instanceName":"1"});
            var Q2809;
            Q2809=makeQuery(id+"F13.opPattern","COPY",BODY,{"derivedFrom":makeQuery(id+"F12.opPattern","COPY",BODY,{"derivedFrom":makeQuery(id+"F11.opPattern","COPY",BODY,{"derivedFrom":makeQuery(id+"F9.opPattern","COPY",BODY,{"derivedFrom":makeQuery(id+"F7.opPattern","COPY",BODY,{"derivedFrom":makeQuery(id+"F3.opPattern","COPY",BODY,{"derivedFrom":makeQuery(id+"F2.opPattern","COPY",BODY,{"derivedFrom":makeQuery(id+"F1.opRevolve","SWEPT_BODY",BODY,{"disambiguationData":[OSD([sQuery(id+"F0.wireOp",EDGE,"E1")])]}),"instanceName":"1"}),"instanceName":"1"}),"instanceName":"1"}),"instanceName":"1"}),"instanceName":"1"}),"instanceName":"1"}),"instanceName":"1"});
            var Q2810;
            Q2810=makeQuery(id+"F13.opPattern","COPY",BODY,{"derivedFrom":makeQuery(id+"F12.opPattern","COPY",BODY,{"derivedFrom":makeQuery(id+"F11.opPattern","COPY",BODY,{"derivedFrom":makeQuery(id+"F9.opPattern","COPY",BODY,{"derivedFrom":makeQuery(id+"F7.opPattern","COPY",BODY,{"derivedFrom":makeQuery(id+"F4.opPattern","COPY",BODY,{"derivedFrom":makeQuery(id+"F1.opRevolve","SWEPT_BODY",BODY,{"disambiguationData":[OSD([sQuery(id+"F0.wireOp",EDGE,"E1")])]}),"instanceName":"1"}),"instanceName":"1"}),"instanceName":"1"}),"instanceName":"1"}),"instanceName":"1"}),"instanceName":"1"});
            var Q2811;
            Q2811=makeQuery(id+"F13.opPattern","COPY",BODY,{"derivedFrom":makeQuery(id+"F12.opPattern","COPY",BODY,{"derivedFrom":makeQuery(id+"F11.opPattern","COPY",BODY,{"derivedFrom":makeQuery(id+"F9.opPattern","COPY",BODY,{"derivedFrom":makeQuery(id+"F7.opPattern","COPY",BODY,{"derivedFrom":makeQuery(id+"F4.opPattern","COPY",BODY,{"derivedFrom":makeQuery(id+"F2.opPattern","COPY",BODY,{"derivedFrom":makeQuery(id+"F1.opRevolve","SWEPT_BODY",BODY,{"disambiguationData":[OSD([sQuery(id+"F0.wireOp",EDGE,"E1")])]}),"instanceName":"1"}),"instanceName":"1"}),"instanceName":"1"}),"instanceName":"1"}),"instanceName":"1"}),"instanceName":"1"}),"instanceName":"1"});
            var Q2812;
            Q2812=makeQuery(id+"F13.opPattern","COPY",BODY,{"derivedFrom":makeQuery(id+"F12.opPattern","COPY",BODY,{"derivedFrom":makeQuery(id+"F11.opPattern","COPY",BODY,{"derivedFrom":makeQuery(id+"F9.opPattern","COPY",BODY,{"derivedFrom":makeQuery(id+"F7.opPattern","COPY",BODY,{"derivedFrom":makeQuery(id+"F4.opPattern","COPY",BODY,{"derivedFrom":makeQuery(id+"F3.opPattern","COPY",BODY,{"derivedFrom":makeQuery(id+"F2.opPattern","COPY",BODY,{"derivedFrom":makeQuery(id+"F1.opRevolve","SWEPT_BODY",BODY,{"disambiguationData":[OSD([sQuery(id+"F0.wireOp",EDGE,"E1")])]}),"instanceName":"1"}),"instanceName":"1"}),"instanceName":"1"}),"instanceName":"1"}),"instanceName":"1"}),"instanceName":"1"}),"instanceName":"1"}),"instanceName":"1"});
            var Q2813;
            Q2813=makeQuery(id+"F13.opPattern","COPY",BODY,{"derivedFrom":makeQuery(id+"F12.opPattern","COPY",BODY,{"derivedFrom":makeQuery(id+"F11.opPattern","COPY",BODY,{"derivedFrom":makeQuery(id+"F9.opPattern","COPY",BODY,{"derivedFrom":makeQuery(id+"F7.opPattern","COPY",BODY,{"derivedFrom":makeQuery(id+"F5.opPattern","COPY",BODY,{"derivedFrom":makeQuery(id+"F1.opRevolve","SWEPT_BODY",BODY,{"disambiguationData":[OSD([sQuery(id+"F0.wireOp",EDGE,"E1")])]}),"instanceName":"1"}),"instanceName":"1"}),"instanceName":"1"}),"instanceName":"1"}),"instanceName":"1"}),"instanceName":"1"});
            var Q2814;
            Q2814=makeQuery(id+"F13.opPattern","COPY",BODY,{"derivedFrom":makeQuery(id+"F12.opPattern","COPY",BODY,{"derivedFrom":makeQuery(id+"F11.opPattern","COPY",BODY,{"derivedFrom":makeQuery(id+"F9.opPattern","COPY",BODY,{"derivedFrom":makeQuery(id+"F7.opPattern","COPY",BODY,{"derivedFrom":makeQuery(id+"F5.opPattern","COPY",BODY,{"derivedFrom":makeQuery(id+"F2.opPattern","COPY",BODY,{"derivedFrom":makeQuery(id+"F1.opRevolve","SWEPT_BODY",BODY,{"disambiguationData":[OSD([sQuery(id+"F0.wireOp",EDGE,"E1")])]}),"instanceName":"1"}),"instanceName":"1"}),"instanceName":"1"}),"instanceName":"1"}),"instanceName":"1"}),"instanceName":"1"}),"instanceName":"1"});
            var Q2815;
            Q2815=makeQuery(id+"F13.opPattern","COPY",BODY,{"derivedFrom":makeQuery(id+"F12.opPattern","COPY",BODY,{"derivedFrom":makeQuery(id+"F11.opPattern","COPY",BODY,{"derivedFrom":makeQuery(id+"F9.opPattern","COPY",BODY,{"derivedFrom":makeQuery(id+"F7.opPattern","COPY",BODY,{"derivedFrom":makeQuery(id+"F5.opPattern","COPY",BODY,{"derivedFrom":makeQuery(id+"F3.opPattern","COPY",BODY,{"derivedFrom":makeQuery(id+"F2.opPattern","COPY",BODY,{"derivedFrom":makeQuery(id+"F1.opRevolve","SWEPT_BODY",BODY,{"disambiguationData":[OSD([sQuery(id+"F0.wireOp",EDGE,"E1")])]}),"instanceName":"1"}),"instanceName":"1"}),"instanceName":"1"}),"instanceName":"1"}),"instanceName":"1"}),"instanceName":"1"}),"instanceName":"1"}),"instanceName":"1"});
            var Q2816;
            Q2816=makeQuery(id+"F13.opPattern","COPY",BODY,{"derivedFrom":makeQuery(id+"F12.opPattern","COPY",BODY,{"derivedFrom":makeQuery(id+"F11.opPattern","COPY",BODY,{"derivedFrom":makeQuery(id+"F9.opPattern","COPY",BODY,{"derivedFrom":makeQuery(id+"F7.opPattern","COPY",BODY,{"derivedFrom":makeQuery(id+"F5.opPattern","COPY",BODY,{"derivedFrom":makeQuery(id+"F4.opPattern","COPY",BODY,{"derivedFrom":makeQuery(id+"F1.opRevolve","SWEPT_BODY",BODY,{"disambiguationData":[OSD([sQuery(id+"F0.wireOp",EDGE,"E1")])]}),"instanceName":"1"}),"instanceName":"1"}),"instanceName":"1"}),"instanceName":"1"}),"instanceName":"1"}),"instanceName":"1"}),"instanceName":"1"});
            var Q2817;
            Q2817=makeQuery(id+"F13.opPattern","COPY",BODY,{"derivedFrom":makeQuery(id+"F12.opPattern","COPY",BODY,{"derivedFrom":makeQuery(id+"F11.opPattern","COPY",BODY,{"derivedFrom":makeQuery(id+"F9.opPattern","COPY",BODY,{"derivedFrom":makeQuery(id+"F7.opPattern","COPY",BODY,{"derivedFrom":makeQuery(id+"F5.opPattern","COPY",BODY,{"derivedFrom":makeQuery(id+"F4.opPattern","COPY",BODY,{"derivedFrom":makeQuery(id+"F2.opPattern","COPY",BODY,{"derivedFrom":makeQuery(id+"F1.opRevolve","SWEPT_BODY",BODY,{"disambiguationData":[OSD([sQuery(id+"F0.wireOp",EDGE,"E1")])]}),"instanceName":"1"}),"instanceName":"1"}),"instanceName":"1"}),"instanceName":"1"}),"instanceName":"1"}),"instanceName":"1"}),"instanceName":"1"}),"instanceName":"1"});
            var Q2818;
            Q2818=makeQuery(id+"F13.opPattern","COPY",BODY,{"derivedFrom":makeQuery(id+"F12.opPattern","COPY",BODY,{"derivedFrom":makeQuery(id+"F11.opPattern","COPY",BODY,{"derivedFrom":makeQuery(id+"F9.opPattern","COPY",BODY,{"derivedFrom":makeQuery(id+"F7.opPattern","COPY",BODY,{"derivedFrom":makeQuery(id+"F5.opPattern","COPY",BODY,{"derivedFrom":makeQuery(id+"F4.opPattern","COPY",BODY,{"derivedFrom":makeQuery(id+"F3.opPattern","COPY",BODY,{"derivedFrom":makeQuery(id+"F2.opPattern","COPY",BODY,{"derivedFrom":makeQuery(id+"F1.opRevolve","SWEPT_BODY",BODY,{"disambiguationData":[OSD([sQuery(id+"F0.wireOp",EDGE,"E1")])]}),"instanceName":"1"}),"instanceName":"1"}),"instanceName":"1"}),"instanceName":"1"}),"instanceName":"1"}),"instanceName":"1"}),"instanceName":"1"}),"instanceName":"1"}),"instanceName":"1"});
            var Q2819;
            Q2819=makeQuery(id+"F13.opPattern","COPY",BODY,{"derivedFrom":makeQuery(id+"F12.opPattern","COPY",BODY,{"derivedFrom":makeQuery(id+"F11.opPattern","COPY",BODY,{"derivedFrom":makeQuery(id+"F9.opPattern","COPY",BODY,{"derivedFrom":makeQuery(id+"F7.opPattern","COPY",BODY,{"derivedFrom":makeQuery(id+"F6.opPattern","COPY",BODY,{"derivedFrom":makeQuery(id+"F1.opRevolve","SWEPT_BODY",BODY,{"disambiguationData":[OSD([sQuery(id+"F0.wireOp",EDGE,"E1")])]}),"instanceName":"1"}),"instanceName":"1"}),"instanceName":"1"}),"instanceName":"1"}),"instanceName":"1"}),"instanceName":"1"});
            var Q2820;
            Q2820=makeQuery(id+"F13.opPattern","COPY",BODY,{"derivedFrom":makeQuery(id+"F12.opPattern","COPY",BODY,{"derivedFrom":makeQuery(id+"F11.opPattern","COPY",BODY,{"derivedFrom":makeQuery(id+"F9.opPattern","COPY",BODY,{"derivedFrom":makeQuery(id+"F7.opPattern","COPY",BODY,{"derivedFrom":makeQuery(id+"F6.opPattern","COPY",BODY,{"derivedFrom":makeQuery(id+"F2.opPattern","COPY",BODY,{"derivedFrom":makeQuery(id+"F1.opRevolve","SWEPT_BODY",BODY,{"disambiguationData":[OSD([sQuery(id+"F0.wireOp",EDGE,"E1")])]}),"instanceName":"1"}),"instanceName":"1"}),"instanceName":"1"}),"instanceName":"1"}),"instanceName":"1"}),"instanceName":"1"}),"instanceName":"1"});
            var Q2821;
            Q2821=makeQuery(id+"F13.opPattern","COPY",BODY,{"derivedFrom":makeQuery(id+"F12.opPattern","COPY",BODY,{"derivedFrom":makeQuery(id+"F11.opPattern","COPY",BODY,{"derivedFrom":makeQuery(id+"F9.opPattern","COPY",BODY,{"derivedFrom":makeQuery(id+"F7.opPattern","COPY",BODY,{"derivedFrom":makeQuery(id+"F6.opPattern","COPY",BODY,{"derivedFrom":makeQuery(id+"F3.opPattern","COPY",BODY,{"derivedFrom":makeQuery(id+"F2.opPattern","COPY",BODY,{"derivedFrom":makeQuery(id+"F1.opRevolve","SWEPT_BODY",BODY,{"disambiguationData":[OSD([sQuery(id+"F0.wireOp",EDGE,"E1")])]}),"instanceName":"1"}),"instanceName":"1"}),"instanceName":"1"}),"instanceName":"1"}),"instanceName":"1"}),"instanceName":"1"}),"instanceName":"1"}),"instanceName":"1"});
            var Q2822;
            Q2822=makeQuery(id+"F13.opPattern","COPY",BODY,{"derivedFrom":makeQuery(id+"F12.opPattern","COPY",BODY,{"derivedFrom":makeQuery(id+"F11.opPattern","COPY",BODY,{"derivedFrom":makeQuery(id+"F9.opPattern","COPY",BODY,{"derivedFrom":makeQuery(id+"F7.opPattern","COPY",BODY,{"derivedFrom":makeQuery(id+"F6.opPattern","COPY",BODY,{"derivedFrom":makeQuery(id+"F4.opPattern","COPY",BODY,{"derivedFrom":makeQuery(id+"F1.opRevolve","SWEPT_BODY",BODY,{"disambiguationData":[OSD([sQuery(id+"F0.wireOp",EDGE,"E1")])]}),"instanceName":"1"}),"instanceName":"1"}),"instanceName":"1"}),"instanceName":"1"}),"instanceName":"1"}),"instanceName":"1"}),"instanceName":"1"});
            var Q2823;
            Q2823=makeQuery(id+"F13.opPattern","COPY",BODY,{"derivedFrom":makeQuery(id+"F12.opPattern","COPY",BODY,{"derivedFrom":makeQuery(id+"F11.opPattern","COPY",BODY,{"derivedFrom":makeQuery(id+"F9.opPattern","COPY",BODY,{"derivedFrom":makeQuery(id+"F7.opPattern","COPY",BODY,{"derivedFrom":makeQuery(id+"F6.opPattern","COPY",BODY,{"derivedFrom":makeQuery(id+"F4.opPattern","COPY",BODY,{"derivedFrom":makeQuery(id+"F2.opPattern","COPY",BODY,{"derivedFrom":makeQuery(id+"F1.opRevolve","SWEPT_BODY",BODY,{"disambiguationData":[OSD([sQuery(id+"F0.wireOp",EDGE,"E1")])]}),"instanceName":"1"}),"instanceName":"1"}),"instanceName":"1"}),"instanceName":"1"}),"instanceName":"1"}),"instanceName":"1"}),"instanceName":"1"}),"instanceName":"1"});
            var Q2824;
            Q2824=makeQuery(id+"F13.opPattern","COPY",BODY,{"derivedFrom":makeQuery(id+"F12.opPattern","COPY",BODY,{"derivedFrom":makeQuery(id+"F11.opPattern","COPY",BODY,{"derivedFrom":makeQuery(id+"F9.opPattern","COPY",BODY,{"derivedFrom":makeQuery(id+"F7.opPattern","COPY",BODY,{"derivedFrom":makeQuery(id+"F6.opPattern","COPY",BODY,{"derivedFrom":makeQuery(id+"F4.opPattern","COPY",BODY,{"derivedFrom":makeQuery(id+"F3.opPattern","COPY",BODY,{"derivedFrom":makeQuery(id+"F2.opPattern","COPY",BODY,{"derivedFrom":makeQuery(id+"F1.opRevolve","SWEPT_BODY",BODY,{"disambiguationData":[OSD([sQuery(id+"F0.wireOp",EDGE,"E1")])]}),"instanceName":"1"}),"instanceName":"1"}),"instanceName":"1"}),"instanceName":"1"}),"instanceName":"1"}),"instanceName":"1"}),"instanceName":"1"}),"instanceName":"1"}),"instanceName":"1"});
            var Q2825;
            Q2825=makeQuery(id+"F13.opPattern","COPY",BODY,{"derivedFrom":makeQuery(id+"F12.opPattern","COPY",BODY,{"derivedFrom":makeQuery(id+"F11.opPattern","COPY",BODY,{"derivedFrom":makeQuery(id+"F9.opPattern","COPY",BODY,{"derivedFrom":makeQuery(id+"F7.opPattern","COPY",BODY,{"derivedFrom":makeQuery(id+"F6.opPattern","COPY",BODY,{"derivedFrom":makeQuery(id+"F5.opPattern","COPY",BODY,{"derivedFrom":makeQuery(id+"F1.opRevolve","SWEPT_BODY",BODY,{"disambiguationData":[OSD([sQuery(id+"F0.wireOp",EDGE,"E1")])]}),"instanceName":"1"}),"instanceName":"1"}),"instanceName":"1"}),"instanceName":"1"}),"instanceName":"1"}),"instanceName":"1"}),"instanceName":"1"});
            var Q2826;
            Q2826=makeQuery(id+"F13.opPattern","COPY",BODY,{"derivedFrom":makeQuery(id+"F12.opPattern","COPY",BODY,{"derivedFrom":makeQuery(id+"F11.opPattern","COPY",BODY,{"derivedFrom":makeQuery(id+"F9.opPattern","COPY",BODY,{"derivedFrom":makeQuery(id+"F7.opPattern","COPY",BODY,{"derivedFrom":makeQuery(id+"F6.opPattern","COPY",BODY,{"derivedFrom":makeQuery(id+"F5.opPattern","COPY",BODY,{"derivedFrom":makeQuery(id+"F2.opPattern","COPY",BODY,{"derivedFrom":makeQuery(id+"F1.opRevolve","SWEPT_BODY",BODY,{"disambiguationData":[OSD([sQuery(id+"F0.wireOp",EDGE,"E1")])]}),"instanceName":"1"}),"instanceName":"1"}),"instanceName":"1"}),"instanceName":"1"}),"instanceName":"1"}),"instanceName":"1"}),"instanceName":"1"}),"instanceName":"1"});
            var Q2827;
            Q2827=makeQuery(id+"F13.opPattern","COPY",BODY,{"derivedFrom":makeQuery(id+"F12.opPattern","COPY",BODY,{"derivedFrom":makeQuery(id+"F11.opPattern","COPY",BODY,{"derivedFrom":makeQuery(id+"F9.opPattern","COPY",BODY,{"derivedFrom":makeQuery(id+"F7.opPattern","COPY",BODY,{"derivedFrom":makeQuery(id+"F6.opPattern","COPY",BODY,{"derivedFrom":makeQuery(id+"F5.opPattern","COPY",BODY,{"derivedFrom":makeQuery(id+"F3.opPattern","COPY",BODY,{"derivedFrom":makeQuery(id+"F2.opPattern","COPY",BODY,{"derivedFrom":makeQuery(id+"F1.opRevolve","SWEPT_BODY",BODY,{"disambiguationData":[OSD([sQuery(id+"F0.wireOp",EDGE,"E1")])]}),"instanceName":"1"}),"instanceName":"1"}),"instanceName":"1"}),"instanceName":"1"}),"instanceName":"1"}),"instanceName":"1"}),"instanceName":"1"}),"instanceName":"1"}),"instanceName":"1"});
            var Q2828;
            Q2828=makeQuery(id+"F13.opPattern","COPY",BODY,{"derivedFrom":makeQuery(id+"F12.opPattern","COPY",BODY,{"derivedFrom":makeQuery(id+"F11.opPattern","COPY",BODY,{"derivedFrom":makeQuery(id+"F9.opPattern","COPY",BODY,{"derivedFrom":makeQuery(id+"F7.opPattern","COPY",BODY,{"derivedFrom":makeQuery(id+"F6.opPattern","COPY",BODY,{"derivedFrom":makeQuery(id+"F5.opPattern","COPY",BODY,{"derivedFrom":makeQuery(id+"F4.opPattern","COPY",BODY,{"derivedFrom":makeQuery(id+"F1.opRevolve","SWEPT_BODY",BODY,{"disambiguationData":[OSD([sQuery(id+"F0.wireOp",EDGE,"E1")])]}),"instanceName":"1"}),"instanceName":"1"}),"instanceName":"1"}),"instanceName":"1"}),"instanceName":"1"}),"instanceName":"1"}),"instanceName":"1"}),"instanceName":"1"});
            var Q2829;
            Q2829=makeQuery(id+"F13.opPattern","COPY",BODY,{"derivedFrom":makeQuery(id+"F12.opPattern","COPY",BODY,{"derivedFrom":makeQuery(id+"F11.opPattern","COPY",BODY,{"derivedFrom":makeQuery(id+"F9.opPattern","COPY",BODY,{"derivedFrom":makeQuery(id+"F7.opPattern","COPY",BODY,{"derivedFrom":makeQuery(id+"F6.opPattern","COPY",BODY,{"derivedFrom":makeQuery(id+"F5.opPattern","COPY",BODY,{"derivedFrom":makeQuery(id+"F4.opPattern","COPY",BODY,{"derivedFrom":makeQuery(id+"F2.opPattern","COPY",BODY,{"derivedFrom":makeQuery(id+"F1.opRevolve","SWEPT_BODY",BODY,{"disambiguationData":[OSD([sQuery(id+"F0.wireOp",EDGE,"E1")])]}),"instanceName":"1"}),"instanceName":"1"}),"instanceName":"1"}),"instanceName":"1"}),"instanceName":"1"}),"instanceName":"1"}),"instanceName":"1"}),"instanceName":"1"}),"instanceName":"1"});
            var Q2830;
            Q2830=makeQuery(id+"F13.opPattern","COPY",BODY,{"derivedFrom":makeQuery(id+"F12.opPattern","COPY",BODY,{"derivedFrom":makeQuery(id+"F11.opPattern","COPY",BODY,{"derivedFrom":makeQuery(id+"F9.opPattern","COPY",BODY,{"derivedFrom":makeQuery(id+"F7.opPattern","COPY",BODY,{"derivedFrom":makeQuery(id+"F6.opPattern","COPY",BODY,{"derivedFrom":makeQuery(id+"F5.opPattern","COPY",BODY,{"derivedFrom":makeQuery(id+"F4.opPattern","COPY",BODY,{"derivedFrom":makeQuery(id+"F3.opPattern","COPY",BODY,{"derivedFrom":makeQuery(id+"F2.opPattern","COPY",BODY,{"derivedFrom":makeQuery(id+"F1.opRevolve","SWEPT_BODY",BODY,{"disambiguationData":[OSD([sQuery(id+"F0.wireOp",EDGE,"E1")])]}),"instanceName":"1"}),"instanceName":"1"}),"instanceName":"1"}),"instanceName":"1"}),"instanceName":"1"}),"instanceName":"1"}),"instanceName":"1"}),"instanceName":"1"}),"instanceName":"1"}),"instanceName":"1"});
            var Q2831;
            Q2831=makeQuery(id+"F13.opPattern","COPY",BODY,{"derivedFrom":makeQuery(id+"F12.opPattern","COPY",BODY,{"derivedFrom":makeQuery(id+"F11.opPattern","COPY",BODY,{"derivedFrom":makeQuery(id+"F9.opPattern","COPY",BODY,{"derivedFrom":makeQuery(id+"F8.opPattern","COPY",BODY,{"derivedFrom":makeQuery(id+"F1.opRevolve","SWEPT_BODY",BODY,{"disambiguationData":[OSD([sQuery(id+"F0.wireOp",EDGE,"E1")])]}),"instanceName":"1"}),"instanceName":"1"}),"instanceName":"1"}),"instanceName":"1"}),"instanceName":"1"});
            var Q2832;
            Q2832=makeQuery(id+"F13.opPattern","COPY",BODY,{"derivedFrom":makeQuery(id+"F12.opPattern","COPY",BODY,{"derivedFrom":makeQuery(id+"F11.opPattern","COPY",BODY,{"derivedFrom":makeQuery(id+"F9.opPattern","COPY",BODY,{"derivedFrom":makeQuery(id+"F8.opPattern","COPY",BODY,{"derivedFrom":makeQuery(id+"F2.opPattern","COPY",BODY,{"derivedFrom":makeQuery(id+"F1.opRevolve","SWEPT_BODY",BODY,{"disambiguationData":[OSD([sQuery(id+"F0.wireOp",EDGE,"E1")])]}),"instanceName":"1"}),"instanceName":"1"}),"instanceName":"1"}),"instanceName":"1"}),"instanceName":"1"}),"instanceName":"1"});
            var Q2833;
            Q2833=makeQuery(id+"F13.opPattern","COPY",BODY,{"derivedFrom":makeQuery(id+"F12.opPattern","COPY",BODY,{"derivedFrom":makeQuery(id+"F11.opPattern","COPY",BODY,{"derivedFrom":makeQuery(id+"F9.opPattern","COPY",BODY,{"derivedFrom":makeQuery(id+"F8.opPattern","COPY",BODY,{"derivedFrom":makeQuery(id+"F3.opPattern","COPY",BODY,{"derivedFrom":makeQuery(id+"F2.opPattern","COPY",BODY,{"derivedFrom":makeQuery(id+"F1.opRevolve","SWEPT_BODY",BODY,{"disambiguationData":[OSD([sQuery(id+"F0.wireOp",EDGE,"E1")])]}),"instanceName":"1"}),"instanceName":"1"}),"instanceName":"1"}),"instanceName":"1"}),"instanceName":"1"}),"instanceName":"1"}),"instanceName":"1"});
            var Q2834;
            Q2834=makeQuery(id+"F13.opPattern","COPY",BODY,{"derivedFrom":makeQuery(id+"F12.opPattern","COPY",BODY,{"derivedFrom":makeQuery(id+"F11.opPattern","COPY",BODY,{"derivedFrom":makeQuery(id+"F9.opPattern","COPY",BODY,{"derivedFrom":makeQuery(id+"F8.opPattern","COPY",BODY,{"derivedFrom":makeQuery(id+"F4.opPattern","COPY",BODY,{"derivedFrom":makeQuery(id+"F1.opRevolve","SWEPT_BODY",BODY,{"disambiguationData":[OSD([sQuery(id+"F0.wireOp",EDGE,"E1")])]}),"instanceName":"1"}),"instanceName":"1"}),"instanceName":"1"}),"instanceName":"1"}),"instanceName":"1"}),"instanceName":"1"});
            var Q2835;
            Q2835=makeQuery(id+"F13.opPattern","COPY",BODY,{"derivedFrom":makeQuery(id+"F12.opPattern","COPY",BODY,{"derivedFrom":makeQuery(id+"F11.opPattern","COPY",BODY,{"derivedFrom":makeQuery(id+"F9.opPattern","COPY",BODY,{"derivedFrom":makeQuery(id+"F8.opPattern","COPY",BODY,{"derivedFrom":makeQuery(id+"F4.opPattern","COPY",BODY,{"derivedFrom":makeQuery(id+"F2.opPattern","COPY",BODY,{"derivedFrom":makeQuery(id+"F1.opRevolve","SWEPT_BODY",BODY,{"disambiguationData":[OSD([sQuery(id+"F0.wireOp",EDGE,"E1")])]}),"instanceName":"1"}),"instanceName":"1"}),"instanceName":"1"}),"instanceName":"1"}),"instanceName":"1"}),"instanceName":"1"}),"instanceName":"1"});
            var Q2836;
            Q2836=makeQuery(id+"F13.opPattern","COPY",BODY,{"derivedFrom":makeQuery(id+"F12.opPattern","COPY",BODY,{"derivedFrom":makeQuery(id+"F11.opPattern","COPY",BODY,{"derivedFrom":makeQuery(id+"F9.opPattern","COPY",BODY,{"derivedFrom":makeQuery(id+"F8.opPattern","COPY",BODY,{"derivedFrom":makeQuery(id+"F4.opPattern","COPY",BODY,{"derivedFrom":makeQuery(id+"F3.opPattern","COPY",BODY,{"derivedFrom":makeQuery(id+"F2.opPattern","COPY",BODY,{"derivedFrom":makeQuery(id+"F1.opRevolve","SWEPT_BODY",BODY,{"disambiguationData":[OSD([sQuery(id+"F0.wireOp",EDGE,"E1")])]}),"instanceName":"1"}),"instanceName":"1"}),"instanceName":"1"}),"instanceName":"1"}),"instanceName":"1"}),"instanceName":"1"}),"instanceName":"1"}),"instanceName":"1"});
            var Q2837;
            Q2837=makeQuery(id+"F13.opPattern","COPY",BODY,{"derivedFrom":makeQuery(id+"F12.opPattern","COPY",BODY,{"derivedFrom":makeQuery(id+"F11.opPattern","COPY",BODY,{"derivedFrom":makeQuery(id+"F9.opPattern","COPY",BODY,{"derivedFrom":makeQuery(id+"F8.opPattern","COPY",BODY,{"derivedFrom":makeQuery(id+"F5.opPattern","COPY",BODY,{"derivedFrom":makeQuery(id+"F1.opRevolve","SWEPT_BODY",BODY,{"disambiguationData":[OSD([sQuery(id+"F0.wireOp",EDGE,"E1")])]}),"instanceName":"1"}),"instanceName":"1"}),"instanceName":"1"}),"instanceName":"1"}),"instanceName":"1"}),"instanceName":"1"});
            var Q2838;
            Q2838=makeQuery(id+"F13.opPattern","COPY",BODY,{"derivedFrom":makeQuery(id+"F12.opPattern","COPY",BODY,{"derivedFrom":makeQuery(id+"F11.opPattern","COPY",BODY,{"derivedFrom":makeQuery(id+"F9.opPattern","COPY",BODY,{"derivedFrom":makeQuery(id+"F8.opPattern","COPY",BODY,{"derivedFrom":makeQuery(id+"F5.opPattern","COPY",BODY,{"derivedFrom":makeQuery(id+"F2.opPattern","COPY",BODY,{"derivedFrom":makeQuery(id+"F1.opRevolve","SWEPT_BODY",BODY,{"disambiguationData":[OSD([sQuery(id+"F0.wireOp",EDGE,"E1")])]}),"instanceName":"1"}),"instanceName":"1"}),"instanceName":"1"}),"instanceName":"1"}),"instanceName":"1"}),"instanceName":"1"}),"instanceName":"1"});
            var Q2839;
            Q2839=makeQuery(id+"F13.opPattern","COPY",BODY,{"derivedFrom":makeQuery(id+"F12.opPattern","COPY",BODY,{"derivedFrom":makeQuery(id+"F11.opPattern","COPY",BODY,{"derivedFrom":makeQuery(id+"F9.opPattern","COPY",BODY,{"derivedFrom":makeQuery(id+"F8.opPattern","COPY",BODY,{"derivedFrom":makeQuery(id+"F5.opPattern","COPY",BODY,{"derivedFrom":makeQuery(id+"F3.opPattern","COPY",BODY,{"derivedFrom":makeQuery(id+"F2.opPattern","COPY",BODY,{"derivedFrom":makeQuery(id+"F1.opRevolve","SWEPT_BODY",BODY,{"disambiguationData":[OSD([sQuery(id+"F0.wireOp",EDGE,"E1")])]}),"instanceName":"1"}),"instanceName":"1"}),"instanceName":"1"}),"instanceName":"1"}),"instanceName":"1"}),"instanceName":"1"}),"instanceName":"1"}),"instanceName":"1"});
            var Q2840;
            Q2840=makeQuery(id+"F13.opPattern","COPY",BODY,{"derivedFrom":makeQuery(id+"F12.opPattern","COPY",BODY,{"derivedFrom":makeQuery(id+"F11.opPattern","COPY",BODY,{"derivedFrom":makeQuery(id+"F9.opPattern","COPY",BODY,{"derivedFrom":makeQuery(id+"F8.opPattern","COPY",BODY,{"derivedFrom":makeQuery(id+"F5.opPattern","COPY",BODY,{"derivedFrom":makeQuery(id+"F4.opPattern","COPY",BODY,{"derivedFrom":makeQuery(id+"F1.opRevolve","SWEPT_BODY",BODY,{"disambiguationData":[OSD([sQuery(id+"F0.wireOp",EDGE,"E1")])]}),"instanceName":"1"}),"instanceName":"1"}),"instanceName":"1"}),"instanceName":"1"}),"instanceName":"1"}),"instanceName":"1"}),"instanceName":"1"});
            var Q2841;
            Q2841=makeQuery(id+"F13.opPattern","COPY",BODY,{"derivedFrom":makeQuery(id+"F12.opPattern","COPY",BODY,{"derivedFrom":makeQuery(id+"F11.opPattern","COPY",BODY,{"derivedFrom":makeQuery(id+"F9.opPattern","COPY",BODY,{"derivedFrom":makeQuery(id+"F8.opPattern","COPY",BODY,{"derivedFrom":makeQuery(id+"F5.opPattern","COPY",BODY,{"derivedFrom":makeQuery(id+"F4.opPattern","COPY",BODY,{"derivedFrom":makeQuery(id+"F2.opPattern","COPY",BODY,{"derivedFrom":makeQuery(id+"F1.opRevolve","SWEPT_BODY",BODY,{"disambiguationData":[OSD([sQuery(id+"F0.wireOp",EDGE,"E1")])]}),"instanceName":"1"}),"instanceName":"1"}),"instanceName":"1"}),"instanceName":"1"}),"instanceName":"1"}),"instanceName":"1"}),"instanceName":"1"}),"instanceName":"1"});
            var Q2842;
            Q2842=makeQuery(id+"F13.opPattern","COPY",BODY,{"derivedFrom":makeQuery(id+"F12.opPattern","COPY",BODY,{"derivedFrom":makeQuery(id+"F11.opPattern","COPY",BODY,{"derivedFrom":makeQuery(id+"F9.opPattern","COPY",BODY,{"derivedFrom":makeQuery(id+"F8.opPattern","COPY",BODY,{"derivedFrom":makeQuery(id+"F5.opPattern","COPY",BODY,{"derivedFrom":makeQuery(id+"F4.opPattern","COPY",BODY,{"derivedFrom":makeQuery(id+"F3.opPattern","COPY",BODY,{"derivedFrom":makeQuery(id+"F2.opPattern","COPY",BODY,{"derivedFrom":makeQuery(id+"F1.opRevolve","SWEPT_BODY",BODY,{"disambiguationData":[OSD([sQuery(id+"F0.wireOp",EDGE,"E1")])]}),"instanceName":"1"}),"instanceName":"1"}),"instanceName":"1"}),"instanceName":"1"}),"instanceName":"1"}),"instanceName":"1"}),"instanceName":"1"}),"instanceName":"1"}),"instanceName":"1"});
            var Q2843;
            Q2843=makeQuery(id+"F13.opPattern","COPY",BODY,{"derivedFrom":makeQuery(id+"F12.opPattern","COPY",BODY,{"derivedFrom":makeQuery(id+"F11.opPattern","COPY",BODY,{"derivedFrom":makeQuery(id+"F9.opPattern","COPY",BODY,{"derivedFrom":makeQuery(id+"F8.opPattern","COPY",BODY,{"derivedFrom":makeQuery(id+"F6.opPattern","COPY",BODY,{"derivedFrom":makeQuery(id+"F1.opRevolve","SWEPT_BODY",BODY,{"disambiguationData":[OSD([sQuery(id+"F0.wireOp",EDGE,"E1")])]}),"instanceName":"1"}),"instanceName":"1"}),"instanceName":"1"}),"instanceName":"1"}),"instanceName":"1"}),"instanceName":"1"});
            var Q2844;
            Q2844=makeQuery(id+"F13.opPattern","COPY",BODY,{"derivedFrom":makeQuery(id+"F12.opPattern","COPY",BODY,{"derivedFrom":makeQuery(id+"F11.opPattern","COPY",BODY,{"derivedFrom":makeQuery(id+"F9.opPattern","COPY",BODY,{"derivedFrom":makeQuery(id+"F8.opPattern","COPY",BODY,{"derivedFrom":makeQuery(id+"F6.opPattern","COPY",BODY,{"derivedFrom":makeQuery(id+"F2.opPattern","COPY",BODY,{"derivedFrom":makeQuery(id+"F1.opRevolve","SWEPT_BODY",BODY,{"disambiguationData":[OSD([sQuery(id+"F0.wireOp",EDGE,"E1")])]}),"instanceName":"1"}),"instanceName":"1"}),"instanceName":"1"}),"instanceName":"1"}),"instanceName":"1"}),"instanceName":"1"}),"instanceName":"1"});
            var Q2845;
            Q2845=makeQuery(id+"F13.opPattern","COPY",BODY,{"derivedFrom":makeQuery(id+"F12.opPattern","COPY",BODY,{"derivedFrom":makeQuery(id+"F11.opPattern","COPY",BODY,{"derivedFrom":makeQuery(id+"F9.opPattern","COPY",BODY,{"derivedFrom":makeQuery(id+"F8.opPattern","COPY",BODY,{"derivedFrom":makeQuery(id+"F6.opPattern","COPY",BODY,{"derivedFrom":makeQuery(id+"F3.opPattern","COPY",BODY,{"derivedFrom":makeQuery(id+"F2.opPattern","COPY",BODY,{"derivedFrom":makeQuery(id+"F1.opRevolve","SWEPT_BODY",BODY,{"disambiguationData":[OSD([sQuery(id+"F0.wireOp",EDGE,"E1")])]}),"instanceName":"1"}),"instanceName":"1"}),"instanceName":"1"}),"instanceName":"1"}),"instanceName":"1"}),"instanceName":"1"}),"instanceName":"1"}),"instanceName":"1"});
            var Q2846;
            Q2846=makeQuery(id+"F13.opPattern","COPY",BODY,{"derivedFrom":makeQuery(id+"F12.opPattern","COPY",BODY,{"derivedFrom":makeQuery(id+"F11.opPattern","COPY",BODY,{"derivedFrom":makeQuery(id+"F9.opPattern","COPY",BODY,{"derivedFrom":makeQuery(id+"F8.opPattern","COPY",BODY,{"derivedFrom":makeQuery(id+"F6.opPattern","COPY",BODY,{"derivedFrom":makeQuery(id+"F4.opPattern","COPY",BODY,{"derivedFrom":makeQuery(id+"F1.opRevolve","SWEPT_BODY",BODY,{"disambiguationData":[OSD([sQuery(id+"F0.wireOp",EDGE,"E1")])]}),"instanceName":"1"}),"instanceName":"1"}),"instanceName":"1"}),"instanceName":"1"}),"instanceName":"1"}),"instanceName":"1"}),"instanceName":"1"});
            var Q2847;
            Q2847=makeQuery(id+"F13.opPattern","COPY",BODY,{"derivedFrom":makeQuery(id+"F12.opPattern","COPY",BODY,{"derivedFrom":makeQuery(id+"F11.opPattern","COPY",BODY,{"derivedFrom":makeQuery(id+"F9.opPattern","COPY",BODY,{"derivedFrom":makeQuery(id+"F8.opPattern","COPY",BODY,{"derivedFrom":makeQuery(id+"F6.opPattern","COPY",BODY,{"derivedFrom":makeQuery(id+"F4.opPattern","COPY",BODY,{"derivedFrom":makeQuery(id+"F2.opPattern","COPY",BODY,{"derivedFrom":makeQuery(id+"F1.opRevolve","SWEPT_BODY",BODY,{"disambiguationData":[OSD([sQuery(id+"F0.wireOp",EDGE,"E1")])]}),"instanceName":"1"}),"instanceName":"1"}),"instanceName":"1"}),"instanceName":"1"}),"instanceName":"1"}),"instanceName":"1"}),"instanceName":"1"}),"instanceName":"1"});
            var Q2848;
            Q2848=makeQuery(id+"F13.opPattern","COPY",BODY,{"derivedFrom":makeQuery(id+"F12.opPattern","COPY",BODY,{"derivedFrom":makeQuery(id+"F11.opPattern","COPY",BODY,{"derivedFrom":makeQuery(id+"F9.opPattern","COPY",BODY,{"derivedFrom":makeQuery(id+"F8.opPattern","COPY",BODY,{"derivedFrom":makeQuery(id+"F6.opPattern","COPY",BODY,{"derivedFrom":makeQuery(id+"F4.opPattern","COPY",BODY,{"derivedFrom":makeQuery(id+"F3.opPattern","COPY",BODY,{"derivedFrom":makeQuery(id+"F2.opPattern","COPY",BODY,{"derivedFrom":makeQuery(id+"F1.opRevolve","SWEPT_BODY",BODY,{"disambiguationData":[OSD([sQuery(id+"F0.wireOp",EDGE,"E1")])]}),"instanceName":"1"}),"instanceName":"1"}),"instanceName":"1"}),"instanceName":"1"}),"instanceName":"1"}),"instanceName":"1"}),"instanceName":"1"}),"instanceName":"1"}),"instanceName":"1"});
            var Q2849;
            Q2849=makeQuery(id+"F13.opPattern","COPY",BODY,{"derivedFrom":makeQuery(id+"F12.opPattern","COPY",BODY,{"derivedFrom":makeQuery(id+"F11.opPattern","COPY",BODY,{"derivedFrom":makeQuery(id+"F9.opPattern","COPY",BODY,{"derivedFrom":makeQuery(id+"F8.opPattern","COPY",BODY,{"derivedFrom":makeQuery(id+"F6.opPattern","COPY",BODY,{"derivedFrom":makeQuery(id+"F5.opPattern","COPY",BODY,{"derivedFrom":makeQuery(id+"F1.opRevolve","SWEPT_BODY",BODY,{"disambiguationData":[OSD([sQuery(id+"F0.wireOp",EDGE,"E1")])]}),"instanceName":"1"}),"instanceName":"1"}),"instanceName":"1"}),"instanceName":"1"}),"instanceName":"1"}),"instanceName":"1"}),"instanceName":"1"});
            var Q2850;
            Q2850=makeQuery(id+"F13.opPattern","COPY",BODY,{"derivedFrom":makeQuery(id+"F12.opPattern","COPY",BODY,{"derivedFrom":makeQuery(id+"F11.opPattern","COPY",BODY,{"derivedFrom":makeQuery(id+"F9.opPattern","COPY",BODY,{"derivedFrom":makeQuery(id+"F8.opPattern","COPY",BODY,{"derivedFrom":makeQuery(id+"F6.opPattern","COPY",BODY,{"derivedFrom":makeQuery(id+"F5.opPattern","COPY",BODY,{"derivedFrom":makeQuery(id+"F2.opPattern","COPY",BODY,{"derivedFrom":makeQuery(id+"F1.opRevolve","SWEPT_BODY",BODY,{"disambiguationData":[OSD([sQuery(id+"F0.wireOp",EDGE,"E1")])]}),"instanceName":"1"}),"instanceName":"1"}),"instanceName":"1"}),"instanceName":"1"}),"instanceName":"1"}),"instanceName":"1"}),"instanceName":"1"}),"instanceName":"1"});
            var Q2851;
            Q2851=makeQuery(id+"F13.opPattern","COPY",BODY,{"derivedFrom":makeQuery(id+"F12.opPattern","COPY",BODY,{"derivedFrom":makeQuery(id+"F11.opPattern","COPY",BODY,{"derivedFrom":makeQuery(id+"F9.opPattern","COPY",BODY,{"derivedFrom":makeQuery(id+"F8.opPattern","COPY",BODY,{"derivedFrom":makeQuery(id+"F6.opPattern","COPY",BODY,{"derivedFrom":makeQuery(id+"F5.opPattern","COPY",BODY,{"derivedFrom":makeQuery(id+"F3.opPattern","COPY",BODY,{"derivedFrom":makeQuery(id+"F2.opPattern","COPY",BODY,{"derivedFrom":makeQuery(id+"F1.opRevolve","SWEPT_BODY",BODY,{"disambiguationData":[OSD([sQuery(id+"F0.wireOp",EDGE,"E1")])]}),"instanceName":"1"}),"instanceName":"1"}),"instanceName":"1"}),"instanceName":"1"}),"instanceName":"1"}),"instanceName":"1"}),"instanceName":"1"}),"instanceName":"1"}),"instanceName":"1"});
            var Q2852;
            Q2852=makeQuery(id+"F13.opPattern","COPY",BODY,{"derivedFrom":makeQuery(id+"F12.opPattern","COPY",BODY,{"derivedFrom":makeQuery(id+"F11.opPattern","COPY",BODY,{"derivedFrom":makeQuery(id+"F9.opPattern","COPY",BODY,{"derivedFrom":makeQuery(id+"F8.opPattern","COPY",BODY,{"derivedFrom":makeQuery(id+"F6.opPattern","COPY",BODY,{"derivedFrom":makeQuery(id+"F5.opPattern","COPY",BODY,{"derivedFrom":makeQuery(id+"F4.opPattern","COPY",BODY,{"derivedFrom":makeQuery(id+"F1.opRevolve","SWEPT_BODY",BODY,{"disambiguationData":[OSD([sQuery(id+"F0.wireOp",EDGE,"E1")])]}),"instanceName":"1"}),"instanceName":"1"}),"instanceName":"1"}),"instanceName":"1"}),"instanceName":"1"}),"instanceName":"1"}),"instanceName":"1"}),"instanceName":"1"});
            var Q2853;
            Q2853=makeQuery(id+"F13.opPattern","COPY",BODY,{"derivedFrom":makeQuery(id+"F12.opPattern","COPY",BODY,{"derivedFrom":makeQuery(id+"F11.opPattern","COPY",BODY,{"derivedFrom":makeQuery(id+"F9.opPattern","COPY",BODY,{"derivedFrom":makeQuery(id+"F8.opPattern","COPY",BODY,{"derivedFrom":makeQuery(id+"F6.opPattern","COPY",BODY,{"derivedFrom":makeQuery(id+"F5.opPattern","COPY",BODY,{"derivedFrom":makeQuery(id+"F4.opPattern","COPY",BODY,{"derivedFrom":makeQuery(id+"F2.opPattern","COPY",BODY,{"derivedFrom":makeQuery(id+"F1.opRevolve","SWEPT_BODY",BODY,{"disambiguationData":[OSD([sQuery(id+"F0.wireOp",EDGE,"E1")])]}),"instanceName":"1"}),"instanceName":"1"}),"instanceName":"1"}),"instanceName":"1"}),"instanceName":"1"}),"instanceName":"1"}),"instanceName":"1"}),"instanceName":"1"}),"instanceName":"1"});
            var Q2854;
            Q2854=makeQuery(id+"F13.opPattern","COPY",BODY,{"derivedFrom":makeQuery(id+"F12.opPattern","COPY",BODY,{"derivedFrom":makeQuery(id+"F11.opPattern","COPY",BODY,{"derivedFrom":makeQuery(id+"F9.opPattern","COPY",BODY,{"derivedFrom":makeQuery(id+"F8.opPattern","COPY",BODY,{"derivedFrom":makeQuery(id+"F6.opPattern","COPY",BODY,{"derivedFrom":makeQuery(id+"F5.opPattern","COPY",BODY,{"derivedFrom":makeQuery(id+"F4.opPattern","COPY",BODY,{"derivedFrom":makeQuery(id+"F3.opPattern","COPY",BODY,{"derivedFrom":makeQuery(id+"F2.opPattern","COPY",BODY,{"derivedFrom":makeQuery(id+"F1.opRevolve","SWEPT_BODY",BODY,{"disambiguationData":[OSD([sQuery(id+"F0.wireOp",EDGE,"E1")])]}),"instanceName":"1"}),"instanceName":"1"}),"instanceName":"1"}),"instanceName":"1"}),"instanceName":"1"}),"instanceName":"1"}),"instanceName":"1"}),"instanceName":"1"}),"instanceName":"1"}),"instanceName":"1"});
            var Q2855;
            Q2855=makeQuery(id+"F13.opPattern","COPY",BODY,{"derivedFrom":makeQuery(id+"F12.opPattern","COPY",BODY,{"derivedFrom":makeQuery(id+"F11.opPattern","COPY",BODY,{"derivedFrom":makeQuery(id+"F9.opPattern","COPY",BODY,{"derivedFrom":makeQuery(id+"F8.opPattern","COPY",BODY,{"derivedFrom":makeQuery(id+"F7.opPattern","COPY",BODY,{"derivedFrom":makeQuery(id+"F1.opRevolve","SWEPT_BODY",BODY,{"disambiguationData":[OSD([sQuery(id+"F0.wireOp",EDGE,"E1")])]}),"instanceName":"1"}),"instanceName":"1"}),"instanceName":"1"}),"instanceName":"1"}),"instanceName":"1"}),"instanceName":"1"});
            var Q2856;
            Q2856=makeQuery(id+"F13.opPattern","COPY",BODY,{"derivedFrom":makeQuery(id+"F12.opPattern","COPY",BODY,{"derivedFrom":makeQuery(id+"F11.opPattern","COPY",BODY,{"derivedFrom":makeQuery(id+"F9.opPattern","COPY",BODY,{"derivedFrom":makeQuery(id+"F8.opPattern","COPY",BODY,{"derivedFrom":makeQuery(id+"F7.opPattern","COPY",BODY,{"derivedFrom":makeQuery(id+"F2.opPattern","COPY",BODY,{"derivedFrom":makeQuery(id+"F1.opRevolve","SWEPT_BODY",BODY,{"disambiguationData":[OSD([sQuery(id+"F0.wireOp",EDGE,"E1")])]}),"instanceName":"1"}),"instanceName":"1"}),"instanceName":"1"}),"instanceName":"1"}),"instanceName":"1"}),"instanceName":"1"}),"instanceName":"1"});
            var Q2857;
            Q2857=makeQuery(id+"F13.opPattern","COPY",BODY,{"derivedFrom":makeQuery(id+"F12.opPattern","COPY",BODY,{"derivedFrom":makeQuery(id+"F11.opPattern","COPY",BODY,{"derivedFrom":makeQuery(id+"F9.opPattern","COPY",BODY,{"derivedFrom":makeQuery(id+"F8.opPattern","COPY",BODY,{"derivedFrom":makeQuery(id+"F7.opPattern","COPY",BODY,{"derivedFrom":makeQuery(id+"F3.opPattern","COPY",BODY,{"derivedFrom":makeQuery(id+"F2.opPattern","COPY",BODY,{"derivedFrom":makeQuery(id+"F1.opRevolve","SWEPT_BODY",BODY,{"disambiguationData":[OSD([sQuery(id+"F0.wireOp",EDGE,"E1")])]}),"instanceName":"1"}),"instanceName":"1"}),"instanceName":"1"}),"instanceName":"1"}),"instanceName":"1"}),"instanceName":"1"}),"instanceName":"1"}),"instanceName":"1"});
            var Q2858;
            Q2858=makeQuery(id+"F13.opPattern","COPY",BODY,{"derivedFrom":makeQuery(id+"F12.opPattern","COPY",BODY,{"derivedFrom":makeQuery(id+"F11.opPattern","COPY",BODY,{"derivedFrom":makeQuery(id+"F9.opPattern","COPY",BODY,{"derivedFrom":makeQuery(id+"F8.opPattern","COPY",BODY,{"derivedFrom":makeQuery(id+"F7.opPattern","COPY",BODY,{"derivedFrom":makeQuery(id+"F4.opPattern","COPY",BODY,{"derivedFrom":makeQuery(id+"F1.opRevolve","SWEPT_BODY",BODY,{"disambiguationData":[OSD([sQuery(id+"F0.wireOp",EDGE,"E1")])]}),"instanceName":"1"}),"instanceName":"1"}),"instanceName":"1"}),"instanceName":"1"}),"instanceName":"1"}),"instanceName":"1"}),"instanceName":"1"});
            var Q2859;
            Q2859=makeQuery(id+"F13.opPattern","COPY",BODY,{"derivedFrom":makeQuery(id+"F12.opPattern","COPY",BODY,{"derivedFrom":makeQuery(id+"F11.opPattern","COPY",BODY,{"derivedFrom":makeQuery(id+"F9.opPattern","COPY",BODY,{"derivedFrom":makeQuery(id+"F8.opPattern","COPY",BODY,{"derivedFrom":makeQuery(id+"F7.opPattern","COPY",BODY,{"derivedFrom":makeQuery(id+"F4.opPattern","COPY",BODY,{"derivedFrom":makeQuery(id+"F2.opPattern","COPY",BODY,{"derivedFrom":makeQuery(id+"F1.opRevolve","SWEPT_BODY",BODY,{"disambiguationData":[OSD([sQuery(id+"F0.wireOp",EDGE,"E1")])]}),"instanceName":"1"}),"instanceName":"1"}),"instanceName":"1"}),"instanceName":"1"}),"instanceName":"1"}),"instanceName":"1"}),"instanceName":"1"}),"instanceName":"1"});
            var Q2860;
            Q2860=makeQuery(id+"F13.opPattern","COPY",BODY,{"derivedFrom":makeQuery(id+"F12.opPattern","COPY",BODY,{"derivedFrom":makeQuery(id+"F11.opPattern","COPY",BODY,{"derivedFrom":makeQuery(id+"F9.opPattern","COPY",BODY,{"derivedFrom":makeQuery(id+"F8.opPattern","COPY",BODY,{"derivedFrom":makeQuery(id+"F7.opPattern","COPY",BODY,{"derivedFrom":makeQuery(id+"F4.opPattern","COPY",BODY,{"derivedFrom":makeQuery(id+"F3.opPattern","COPY",BODY,{"derivedFrom":makeQuery(id+"F2.opPattern","COPY",BODY,{"derivedFrom":makeQuery(id+"F1.opRevolve","SWEPT_BODY",BODY,{"disambiguationData":[OSD([sQuery(id+"F0.wireOp",EDGE,"E1")])]}),"instanceName":"1"}),"instanceName":"1"}),"instanceName":"1"}),"instanceName":"1"}),"instanceName":"1"}),"instanceName":"1"}),"instanceName":"1"}),"instanceName":"1"}),"instanceName":"1"});
            var Q2861;
            Q2861=makeQuery(id+"F13.opPattern","COPY",BODY,{"derivedFrom":makeQuery(id+"F12.opPattern","COPY",BODY,{"derivedFrom":makeQuery(id+"F11.opPattern","COPY",BODY,{"derivedFrom":makeQuery(id+"F9.opPattern","COPY",BODY,{"derivedFrom":makeQuery(id+"F8.opPattern","COPY",BODY,{"derivedFrom":makeQuery(id+"F7.opPattern","COPY",BODY,{"derivedFrom":makeQuery(id+"F5.opPattern","COPY",BODY,{"derivedFrom":makeQuery(id+"F1.opRevolve","SWEPT_BODY",BODY,{"disambiguationData":[OSD([sQuery(id+"F0.wireOp",EDGE,"E1")])]}),"instanceName":"1"}),"instanceName":"1"}),"instanceName":"1"}),"instanceName":"1"}),"instanceName":"1"}),"instanceName":"1"}),"instanceName":"1"});
            var Q2862;
            Q2862=makeQuery(id+"F13.opPattern","COPY",BODY,{"derivedFrom":makeQuery(id+"F12.opPattern","COPY",BODY,{"derivedFrom":makeQuery(id+"F11.opPattern","COPY",BODY,{"derivedFrom":makeQuery(id+"F9.opPattern","COPY",BODY,{"derivedFrom":makeQuery(id+"F8.opPattern","COPY",BODY,{"derivedFrom":makeQuery(id+"F7.opPattern","COPY",BODY,{"derivedFrom":makeQuery(id+"F5.opPattern","COPY",BODY,{"derivedFrom":makeQuery(id+"F2.opPattern","COPY",BODY,{"derivedFrom":makeQuery(id+"F1.opRevolve","SWEPT_BODY",BODY,{"disambiguationData":[OSD([sQuery(id+"F0.wireOp",EDGE,"E1")])]}),"instanceName":"1"}),"instanceName":"1"}),"instanceName":"1"}),"instanceName":"1"}),"instanceName":"1"}),"instanceName":"1"}),"instanceName":"1"}),"instanceName":"1"});
            var Q2863;
            Q2863=makeQuery(id+"F13.opPattern","COPY",BODY,{"derivedFrom":makeQuery(id+"F12.opPattern","COPY",BODY,{"derivedFrom":makeQuery(id+"F11.opPattern","COPY",BODY,{"derivedFrom":makeQuery(id+"F9.opPattern","COPY",BODY,{"derivedFrom":makeQuery(id+"F8.opPattern","COPY",BODY,{"derivedFrom":makeQuery(id+"F7.opPattern","COPY",BODY,{"derivedFrom":makeQuery(id+"F5.opPattern","COPY",BODY,{"derivedFrom":makeQuery(id+"F3.opPattern","COPY",BODY,{"derivedFrom":makeQuery(id+"F2.opPattern","COPY",BODY,{"derivedFrom":makeQuery(id+"F1.opRevolve","SWEPT_BODY",BODY,{"disambiguationData":[OSD([sQuery(id+"F0.wireOp",EDGE,"E1")])]}),"instanceName":"1"}),"instanceName":"1"}),"instanceName":"1"}),"instanceName":"1"}),"instanceName":"1"}),"instanceName":"1"}),"instanceName":"1"}),"instanceName":"1"}),"instanceName":"1"});
            var Q2864;
            Q2864=makeQuery(id+"F13.opPattern","COPY",BODY,{"derivedFrom":makeQuery(id+"F12.opPattern","COPY",BODY,{"derivedFrom":makeQuery(id+"F11.opPattern","COPY",BODY,{"derivedFrom":makeQuery(id+"F9.opPattern","COPY",BODY,{"derivedFrom":makeQuery(id+"F8.opPattern","COPY",BODY,{"derivedFrom":makeQuery(id+"F7.opPattern","COPY",BODY,{"derivedFrom":makeQuery(id+"F5.opPattern","COPY",BODY,{"derivedFrom":makeQuery(id+"F4.opPattern","COPY",BODY,{"derivedFrom":makeQuery(id+"F1.opRevolve","SWEPT_BODY",BODY,{"disambiguationData":[OSD([sQuery(id+"F0.wireOp",EDGE,"E1")])]}),"instanceName":"1"}),"instanceName":"1"}),"instanceName":"1"}),"instanceName":"1"}),"instanceName":"1"}),"instanceName":"1"}),"instanceName":"1"}),"instanceName":"1"});
            var Q2865;
            Q2865=makeQuery(id+"F13.opPattern","COPY",BODY,{"derivedFrom":makeQuery(id+"F12.opPattern","COPY",BODY,{"derivedFrom":makeQuery(id+"F11.opPattern","COPY",BODY,{"derivedFrom":makeQuery(id+"F9.opPattern","COPY",BODY,{"derivedFrom":makeQuery(id+"F8.opPattern","COPY",BODY,{"derivedFrom":makeQuery(id+"F7.opPattern","COPY",BODY,{"derivedFrom":makeQuery(id+"F5.opPattern","COPY",BODY,{"derivedFrom":makeQuery(id+"F4.opPattern","COPY",BODY,{"derivedFrom":makeQuery(id+"F2.opPattern","COPY",BODY,{"derivedFrom":makeQuery(id+"F1.opRevolve","SWEPT_BODY",BODY,{"disambiguationData":[OSD([sQuery(id+"F0.wireOp",EDGE,"E1")])]}),"instanceName":"1"}),"instanceName":"1"}),"instanceName":"1"}),"instanceName":"1"}),"instanceName":"1"}),"instanceName":"1"}),"instanceName":"1"}),"instanceName":"1"}),"instanceName":"1"});
            var Q2866;
            Q2866=makeQuery(id+"F13.opPattern","COPY",BODY,{"derivedFrom":makeQuery(id+"F12.opPattern","COPY",BODY,{"derivedFrom":makeQuery(id+"F11.opPattern","COPY",BODY,{"derivedFrom":makeQuery(id+"F9.opPattern","COPY",BODY,{"derivedFrom":makeQuery(id+"F8.opPattern","COPY",BODY,{"derivedFrom":makeQuery(id+"F7.opPattern","COPY",BODY,{"derivedFrom":makeQuery(id+"F5.opPattern","COPY",BODY,{"derivedFrom":makeQuery(id+"F4.opPattern","COPY",BODY,{"derivedFrom":makeQuery(id+"F3.opPattern","COPY",BODY,{"derivedFrom":makeQuery(id+"F2.opPattern","COPY",BODY,{"derivedFrom":makeQuery(id+"F1.opRevolve","SWEPT_BODY",BODY,{"disambiguationData":[OSD([sQuery(id+"F0.wireOp",EDGE,"E1")])]}),"instanceName":"1"}),"instanceName":"1"}),"instanceName":"1"}),"instanceName":"1"}),"instanceName":"1"}),"instanceName":"1"}),"instanceName":"1"}),"instanceName":"1"}),"instanceName":"1"}),"instanceName":"1"});
            var Q2867;
            Q2867=makeQuery(id+"F13.opPattern","COPY",BODY,{"derivedFrom":makeQuery(id+"F12.opPattern","COPY",BODY,{"derivedFrom":makeQuery(id+"F11.opPattern","COPY",BODY,{"derivedFrom":makeQuery(id+"F9.opPattern","COPY",BODY,{"derivedFrom":makeQuery(id+"F8.opPattern","COPY",BODY,{"derivedFrom":makeQuery(id+"F7.opPattern","COPY",BODY,{"derivedFrom":makeQuery(id+"F6.opPattern","COPY",BODY,{"derivedFrom":makeQuery(id+"F1.opRevolve","SWEPT_BODY",BODY,{"disambiguationData":[OSD([sQuery(id+"F0.wireOp",EDGE,"E1")])]}),"instanceName":"1"}),"instanceName":"1"}),"instanceName":"1"}),"instanceName":"1"}),"instanceName":"1"}),"instanceName":"1"}),"instanceName":"1"});
            var Q2868;
            Q2868=makeQuery(id+"F13.opPattern","COPY",BODY,{"derivedFrom":makeQuery(id+"F12.opPattern","COPY",BODY,{"derivedFrom":makeQuery(id+"F11.opPattern","COPY",BODY,{"derivedFrom":makeQuery(id+"F9.opPattern","COPY",BODY,{"derivedFrom":makeQuery(id+"F8.opPattern","COPY",BODY,{"derivedFrom":makeQuery(id+"F7.opPattern","COPY",BODY,{"derivedFrom":makeQuery(id+"F6.opPattern","COPY",BODY,{"derivedFrom":makeQuery(id+"F2.opPattern","COPY",BODY,{"derivedFrom":makeQuery(id+"F1.opRevolve","SWEPT_BODY",BODY,{"disambiguationData":[OSD([sQuery(id+"F0.wireOp",EDGE,"E1")])]}),"instanceName":"1"}),"instanceName":"1"}),"instanceName":"1"}),"instanceName":"1"}),"instanceName":"1"}),"instanceName":"1"}),"instanceName":"1"}),"instanceName":"1"});
            var Q2869;
            Q2869=makeQuery(id+"F13.opPattern","COPY",BODY,{"derivedFrom":makeQuery(id+"F12.opPattern","COPY",BODY,{"derivedFrom":makeQuery(id+"F11.opPattern","COPY",BODY,{"derivedFrom":makeQuery(id+"F9.opPattern","COPY",BODY,{"derivedFrom":makeQuery(id+"F8.opPattern","COPY",BODY,{"derivedFrom":makeQuery(id+"F7.opPattern","COPY",BODY,{"derivedFrom":makeQuery(id+"F6.opPattern","COPY",BODY,{"derivedFrom":makeQuery(id+"F3.opPattern","COPY",BODY,{"derivedFrom":makeQuery(id+"F2.opPattern","COPY",BODY,{"derivedFrom":makeQuery(id+"F1.opRevolve","SWEPT_BODY",BODY,{"disambiguationData":[OSD([sQuery(id+"F0.wireOp",EDGE,"E1")])]}),"instanceName":"1"}),"instanceName":"1"}),"instanceName":"1"}),"instanceName":"1"}),"instanceName":"1"}),"instanceName":"1"}),"instanceName":"1"}),"instanceName":"1"}),"instanceName":"1"});
            var Q2870;
            Q2870=makeQuery(id+"F13.opPattern","COPY",BODY,{"derivedFrom":makeQuery(id+"F12.opPattern","COPY",BODY,{"derivedFrom":makeQuery(id+"F11.opPattern","COPY",BODY,{"derivedFrom":makeQuery(id+"F9.opPattern","COPY",BODY,{"derivedFrom":makeQuery(id+"F8.opPattern","COPY",BODY,{"derivedFrom":makeQuery(id+"F7.opPattern","COPY",BODY,{"derivedFrom":makeQuery(id+"F6.opPattern","COPY",BODY,{"derivedFrom":makeQuery(id+"F4.opPattern","COPY",BODY,{"derivedFrom":makeQuery(id+"F1.opRevolve","SWEPT_BODY",BODY,{"disambiguationData":[OSD([sQuery(id+"F0.wireOp",EDGE,"E1")])]}),"instanceName":"1"}),"instanceName":"1"}),"instanceName":"1"}),"instanceName":"1"}),"instanceName":"1"}),"instanceName":"1"}),"instanceName":"1"}),"instanceName":"1"});
            var Q2871;
            Q2871=makeQuery(id+"F13.opPattern","COPY",BODY,{"derivedFrom":makeQuery(id+"F12.opPattern","COPY",BODY,{"derivedFrom":makeQuery(id+"F11.opPattern","COPY",BODY,{"derivedFrom":makeQuery(id+"F9.opPattern","COPY",BODY,{"derivedFrom":makeQuery(id+"F8.opPattern","COPY",BODY,{"derivedFrom":makeQuery(id+"F7.opPattern","COPY",BODY,{"derivedFrom":makeQuery(id+"F6.opPattern","COPY",BODY,{"derivedFrom":makeQuery(id+"F4.opPattern","COPY",BODY,{"derivedFrom":makeQuery(id+"F2.opPattern","COPY",BODY,{"derivedFrom":makeQuery(id+"F1.opRevolve","SWEPT_BODY",BODY,{"disambiguationData":[OSD([sQuery(id+"F0.wireOp",EDGE,"E1")])]}),"instanceName":"1"}),"instanceName":"1"}),"instanceName":"1"}),"instanceName":"1"}),"instanceName":"1"}),"instanceName":"1"}),"instanceName":"1"}),"instanceName":"1"}),"instanceName":"1"});
            var Q2872;
            Q2872=makeQuery(id+"F13.opPattern","COPY",BODY,{"derivedFrom":makeQuery(id+"F12.opPattern","COPY",BODY,{"derivedFrom":makeQuery(id+"F11.opPattern","COPY",BODY,{"derivedFrom":makeQuery(id+"F9.opPattern","COPY",BODY,{"derivedFrom":makeQuery(id+"F8.opPattern","COPY",BODY,{"derivedFrom":makeQuery(id+"F7.opPattern","COPY",BODY,{"derivedFrom":makeQuery(id+"F6.opPattern","COPY",BODY,{"derivedFrom":makeQuery(id+"F4.opPattern","COPY",BODY,{"derivedFrom":makeQuery(id+"F3.opPattern","COPY",BODY,{"derivedFrom":makeQuery(id+"F2.opPattern","COPY",BODY,{"derivedFrom":makeQuery(id+"F1.opRevolve","SWEPT_BODY",BODY,{"disambiguationData":[OSD([sQuery(id+"F0.wireOp",EDGE,"E1")])]}),"instanceName":"1"}),"instanceName":"1"}),"instanceName":"1"}),"instanceName":"1"}),"instanceName":"1"}),"instanceName":"1"}),"instanceName":"1"}),"instanceName":"1"}),"instanceName":"1"}),"instanceName":"1"});
            var Q2873;
            Q2873=makeQuery(id+"F13.opPattern","COPY",BODY,{"derivedFrom":makeQuery(id+"F12.opPattern","COPY",BODY,{"derivedFrom":makeQuery(id+"F11.opPattern","COPY",BODY,{"derivedFrom":makeQuery(id+"F9.opPattern","COPY",BODY,{"derivedFrom":makeQuery(id+"F8.opPattern","COPY",BODY,{"derivedFrom":makeQuery(id+"F7.opPattern","COPY",BODY,{"derivedFrom":makeQuery(id+"F6.opPattern","COPY",BODY,{"derivedFrom":makeQuery(id+"F5.opPattern","COPY",BODY,{"derivedFrom":makeQuery(id+"F1.opRevolve","SWEPT_BODY",BODY,{"disambiguationData":[OSD([sQuery(id+"F0.wireOp",EDGE,"E1")])]}),"instanceName":"1"}),"instanceName":"1"}),"instanceName":"1"}),"instanceName":"1"}),"instanceName":"1"}),"instanceName":"1"}),"instanceName":"1"}),"instanceName":"1"});
            var Q2874;
            Q2874=makeQuery(id+"F13.opPattern","COPY",BODY,{"derivedFrom":makeQuery(id+"F12.opPattern","COPY",BODY,{"derivedFrom":makeQuery(id+"F11.opPattern","COPY",BODY,{"derivedFrom":makeQuery(id+"F9.opPattern","COPY",BODY,{"derivedFrom":makeQuery(id+"F8.opPattern","COPY",BODY,{"derivedFrom":makeQuery(id+"F7.opPattern","COPY",BODY,{"derivedFrom":makeQuery(id+"F6.opPattern","COPY",BODY,{"derivedFrom":makeQuery(id+"F5.opPattern","COPY",BODY,{"derivedFrom":makeQuery(id+"F2.opPattern","COPY",BODY,{"derivedFrom":makeQuery(id+"F1.opRevolve","SWEPT_BODY",BODY,{"disambiguationData":[OSD([sQuery(id+"F0.wireOp",EDGE,"E1")])]}),"instanceName":"1"}),"instanceName":"1"}),"instanceName":"1"}),"instanceName":"1"}),"instanceName":"1"}),"instanceName":"1"}),"instanceName":"1"}),"instanceName":"1"}),"instanceName":"1"});
            var Q2875;
            Q2875=makeQuery(id+"F13.opPattern","COPY",BODY,{"derivedFrom":makeQuery(id+"F12.opPattern","COPY",BODY,{"derivedFrom":makeQuery(id+"F11.opPattern","COPY",BODY,{"derivedFrom":makeQuery(id+"F9.opPattern","COPY",BODY,{"derivedFrom":makeQuery(id+"F8.opPattern","COPY",BODY,{"derivedFrom":makeQuery(id+"F7.opPattern","COPY",BODY,{"derivedFrom":makeQuery(id+"F6.opPattern","COPY",BODY,{"derivedFrom":makeQuery(id+"F5.opPattern","COPY",BODY,{"derivedFrom":makeQuery(id+"F3.opPattern","COPY",BODY,{"derivedFrom":makeQuery(id+"F2.opPattern","COPY",BODY,{"derivedFrom":makeQuery(id+"F1.opRevolve","SWEPT_BODY",BODY,{"disambiguationData":[OSD([sQuery(id+"F0.wireOp",EDGE,"E1")])]}),"instanceName":"1"}),"instanceName":"1"}),"instanceName":"1"}),"instanceName":"1"}),"instanceName":"1"}),"instanceName":"1"}),"instanceName":"1"}),"instanceName":"1"}),"instanceName":"1"}),"instanceName":"1"});
            var Q2876;
            Q2876=makeQuery(id+"F13.opPattern","COPY",BODY,{"derivedFrom":makeQuery(id+"F12.opPattern","COPY",BODY,{"derivedFrom":makeQuery(id+"F11.opPattern","COPY",BODY,{"derivedFrom":makeQuery(id+"F9.opPattern","COPY",BODY,{"derivedFrom":makeQuery(id+"F8.opPattern","COPY",BODY,{"derivedFrom":makeQuery(id+"F7.opPattern","COPY",BODY,{"derivedFrom":makeQuery(id+"F6.opPattern","COPY",BODY,{"derivedFrom":makeQuery(id+"F5.opPattern","COPY",BODY,{"derivedFrom":makeQuery(id+"F4.opPattern","COPY",BODY,{"derivedFrom":makeQuery(id+"F1.opRevolve","SWEPT_BODY",BODY,{"disambiguationData":[OSD([sQuery(id+"F0.wireOp",EDGE,"E1")])]}),"instanceName":"1"}),"instanceName":"1"}),"instanceName":"1"}),"instanceName":"1"}),"instanceName":"1"}),"instanceName":"1"}),"instanceName":"1"}),"instanceName":"1"}),"instanceName":"1"});
            var Q2877;
            Q2877=makeQuery(id+"F13.opPattern","COPY",BODY,{"derivedFrom":makeQuery(id+"F12.opPattern","COPY",BODY,{"derivedFrom":makeQuery(id+"F11.opPattern","COPY",BODY,{"derivedFrom":makeQuery(id+"F9.opPattern","COPY",BODY,{"derivedFrom":makeQuery(id+"F8.opPattern","COPY",BODY,{"derivedFrom":makeQuery(id+"F7.opPattern","COPY",BODY,{"derivedFrom":makeQuery(id+"F6.opPattern","COPY",BODY,{"derivedFrom":makeQuery(id+"F5.opPattern","COPY",BODY,{"derivedFrom":makeQuery(id+"F4.opPattern","COPY",BODY,{"derivedFrom":makeQuery(id+"F2.opPattern","COPY",BODY,{"derivedFrom":makeQuery(id+"F1.opRevolve","SWEPT_BODY",BODY,{"disambiguationData":[OSD([sQuery(id+"F0.wireOp",EDGE,"E1")])]}),"instanceName":"1"}),"instanceName":"1"}),"instanceName":"1"}),"instanceName":"1"}),"instanceName":"1"}),"instanceName":"1"}),"instanceName":"1"}),"instanceName":"1"}),"instanceName":"1"}),"instanceName":"1"});
            var Q2878;
            Q2878=makeQuery(id+"F13.opPattern","COPY",BODY,{"derivedFrom":makeQuery(id+"F12.opPattern","COPY",BODY,{"derivedFrom":makeQuery(id+"F11.opPattern","COPY",BODY,{"derivedFrom":makeQuery(id+"F9.opPattern","COPY",BODY,{"derivedFrom":makeQuery(id+"F8.opPattern","COPY",BODY,{"derivedFrom":makeQuery(id+"F7.opPattern","COPY",BODY,{"derivedFrom":makeQuery(id+"F6.opPattern","COPY",BODY,{"derivedFrom":makeQuery(id+"F5.opPattern","COPY",BODY,{"derivedFrom":makeQuery(id+"F4.opPattern","COPY",BODY,{"derivedFrom":makeQuery(id+"F3.opPattern","COPY",BODY,{"derivedFrom":makeQuery(id+"F2.opPattern","COPY",BODY,{"derivedFrom":makeQuery(id+"F1.opRevolve","SWEPT_BODY",BODY,{"disambiguationData":[OSD([sQuery(id+"F0.wireOp",EDGE,"E1")])]}),"instanceName":"1"}),"instanceName":"1"}),"instanceName":"1"}),"instanceName":"1"}),"instanceName":"1"}),"instanceName":"1"}),"instanceName":"1"}),"instanceName":"1"}),"instanceName":"1"}),"instanceName":"1"}),"instanceName":"1"});
            var Q2879;
            Q2879=makeQuery(id+"F13.opPattern","COPY",BODY,{"derivedFrom":makeQuery(id+"F12.opPattern","COPY",BODY,{"derivedFrom":makeQuery(id+"F11.opPattern","COPY",BODY,{"derivedFrom":makeQuery(id+"F10.opPattern","COPY",BODY,{"derivedFrom":makeQuery(id+"F1.opRevolve","SWEPT_BODY",BODY,{"disambiguationData":[OSD([sQuery(id+"F0.wireOp",EDGE,"E1")])]}),"instanceName":"1"}),"instanceName":"1"}),"instanceName":"1"}),"instanceName":"1"});
            var Q2880;
            Q2880=makeQuery(id+"F13.opPattern","COPY",BODY,{"derivedFrom":makeQuery(id+"F12.opPattern","COPY",BODY,{"derivedFrom":makeQuery(id+"F11.opPattern","COPY",BODY,{"derivedFrom":makeQuery(id+"F10.opPattern","COPY",BODY,{"derivedFrom":makeQuery(id+"F2.opPattern","COPY",BODY,{"derivedFrom":makeQuery(id+"F1.opRevolve","SWEPT_BODY",BODY,{"disambiguationData":[OSD([sQuery(id+"F0.wireOp",EDGE,"E1")])]}),"instanceName":"1"}),"instanceName":"1"}),"instanceName":"1"}),"instanceName":"1"}),"instanceName":"1"});
            var Q2881;
            Q2881=makeQuery(id+"F13.opPattern","COPY",BODY,{"derivedFrom":makeQuery(id+"F12.opPattern","COPY",BODY,{"derivedFrom":makeQuery(id+"F11.opPattern","COPY",BODY,{"derivedFrom":makeQuery(id+"F10.opPattern","COPY",BODY,{"derivedFrom":makeQuery(id+"F3.opPattern","COPY",BODY,{"derivedFrom":makeQuery(id+"F2.opPattern","COPY",BODY,{"derivedFrom":makeQuery(id+"F1.opRevolve","SWEPT_BODY",BODY,{"disambiguationData":[OSD([sQuery(id+"F0.wireOp",EDGE,"E1")])]}),"instanceName":"1"}),"instanceName":"1"}),"instanceName":"1"}),"instanceName":"1"}),"instanceName":"1"}),"instanceName":"1"});
            var Q2882;
            Q2882=makeQuery(id+"F13.opPattern","COPY",BODY,{"derivedFrom":makeQuery(id+"F12.opPattern","COPY",BODY,{"derivedFrom":makeQuery(id+"F11.opPattern","COPY",BODY,{"derivedFrom":makeQuery(id+"F10.opPattern","COPY",BODY,{"derivedFrom":makeQuery(id+"F4.opPattern","COPY",BODY,{"derivedFrom":makeQuery(id+"F1.opRevolve","SWEPT_BODY",BODY,{"disambiguationData":[OSD([sQuery(id+"F0.wireOp",EDGE,"E1")])]}),"instanceName":"1"}),"instanceName":"1"}),"instanceName":"1"}),"instanceName":"1"}),"instanceName":"1"});
            var Q2883;
            Q2883=makeQuery(id+"F13.opPattern","COPY",BODY,{"derivedFrom":makeQuery(id+"F12.opPattern","COPY",BODY,{"derivedFrom":makeQuery(id+"F11.opPattern","COPY",BODY,{"derivedFrom":makeQuery(id+"F10.opPattern","COPY",BODY,{"derivedFrom":makeQuery(id+"F4.opPattern","COPY",BODY,{"derivedFrom":makeQuery(id+"F2.opPattern","COPY",BODY,{"derivedFrom":makeQuery(id+"F1.opRevolve","SWEPT_BODY",BODY,{"disambiguationData":[OSD([sQuery(id+"F0.wireOp",EDGE,"E1")])]}),"instanceName":"1"}),"instanceName":"1"}),"instanceName":"1"}),"instanceName":"1"}),"instanceName":"1"}),"instanceName":"1"});
            var Q2884;
            Q2884=makeQuery(id+"F13.opPattern","COPY",BODY,{"derivedFrom":makeQuery(id+"F12.opPattern","COPY",BODY,{"derivedFrom":makeQuery(id+"F11.opPattern","COPY",BODY,{"derivedFrom":makeQuery(id+"F10.opPattern","COPY",BODY,{"derivedFrom":makeQuery(id+"F4.opPattern","COPY",BODY,{"derivedFrom":makeQuery(id+"F3.opPattern","COPY",BODY,{"derivedFrom":makeQuery(id+"F2.opPattern","COPY",BODY,{"derivedFrom":makeQuery(id+"F1.opRevolve","SWEPT_BODY",BODY,{"disambiguationData":[OSD([sQuery(id+"F0.wireOp",EDGE,"E1")])]}),"instanceName":"1"}),"instanceName":"1"}),"instanceName":"1"}),"instanceName":"1"}),"instanceName":"1"}),"instanceName":"1"}),"instanceName":"1"});
            var Q2885;
            Q2885=makeQuery(id+"F13.opPattern","COPY",BODY,{"derivedFrom":makeQuery(id+"F12.opPattern","COPY",BODY,{"derivedFrom":makeQuery(id+"F11.opPattern","COPY",BODY,{"derivedFrom":makeQuery(id+"F10.opPattern","COPY",BODY,{"derivedFrom":makeQuery(id+"F5.opPattern","COPY",BODY,{"derivedFrom":makeQuery(id+"F1.opRevolve","SWEPT_BODY",BODY,{"disambiguationData":[OSD([sQuery(id+"F0.wireOp",EDGE,"E1")])]}),"instanceName":"1"}),"instanceName":"1"}),"instanceName":"1"}),"instanceName":"1"}),"instanceName":"1"});
            var Q2886;
            Q2886=makeQuery(id+"F13.opPattern","COPY",BODY,{"derivedFrom":makeQuery(id+"F12.opPattern","COPY",BODY,{"derivedFrom":makeQuery(id+"F11.opPattern","COPY",BODY,{"derivedFrom":makeQuery(id+"F10.opPattern","COPY",BODY,{"derivedFrom":makeQuery(id+"F5.opPattern","COPY",BODY,{"derivedFrom":makeQuery(id+"F2.opPattern","COPY",BODY,{"derivedFrom":makeQuery(id+"F1.opRevolve","SWEPT_BODY",BODY,{"disambiguationData":[OSD([sQuery(id+"F0.wireOp",EDGE,"E1")])]}),"instanceName":"1"}),"instanceName":"1"}),"instanceName":"1"}),"instanceName":"1"}),"instanceName":"1"}),"instanceName":"1"});
            var Q2887;
            Q2887=makeQuery(id+"F13.opPattern","COPY",BODY,{"derivedFrom":makeQuery(id+"F12.opPattern","COPY",BODY,{"derivedFrom":makeQuery(id+"F11.opPattern","COPY",BODY,{"derivedFrom":makeQuery(id+"F10.opPattern","COPY",BODY,{"derivedFrom":makeQuery(id+"F5.opPattern","COPY",BODY,{"derivedFrom":makeQuery(id+"F3.opPattern","COPY",BODY,{"derivedFrom":makeQuery(id+"F2.opPattern","COPY",BODY,{"derivedFrom":makeQuery(id+"F1.opRevolve","SWEPT_BODY",BODY,{"disambiguationData":[OSD([sQuery(id+"F0.wireOp",EDGE,"E1")])]}),"instanceName":"1"}),"instanceName":"1"}),"instanceName":"1"}),"instanceName":"1"}),"instanceName":"1"}),"instanceName":"1"}),"instanceName":"1"});
            var Q2888;
            Q2888=makeQuery(id+"F13.opPattern","COPY",BODY,{"derivedFrom":makeQuery(id+"F12.opPattern","COPY",BODY,{"derivedFrom":makeQuery(id+"F11.opPattern","COPY",BODY,{"derivedFrom":makeQuery(id+"F10.opPattern","COPY",BODY,{"derivedFrom":makeQuery(id+"F5.opPattern","COPY",BODY,{"derivedFrom":makeQuery(id+"F4.opPattern","COPY",BODY,{"derivedFrom":makeQuery(id+"F1.opRevolve","SWEPT_BODY",BODY,{"disambiguationData":[OSD([sQuery(id+"F0.wireOp",EDGE,"E1")])]}),"instanceName":"1"}),"instanceName":"1"}),"instanceName":"1"}),"instanceName":"1"}),"instanceName":"1"}),"instanceName":"1"});
            var Q2889;
            Q2889=makeQuery(id+"F13.opPattern","COPY",BODY,{"derivedFrom":makeQuery(id+"F12.opPattern","COPY",BODY,{"derivedFrom":makeQuery(id+"F11.opPattern","COPY",BODY,{"derivedFrom":makeQuery(id+"F10.opPattern","COPY",BODY,{"derivedFrom":makeQuery(id+"F5.opPattern","COPY",BODY,{"derivedFrom":makeQuery(id+"F4.opPattern","COPY",BODY,{"derivedFrom":makeQuery(id+"F2.opPattern","COPY",BODY,{"derivedFrom":makeQuery(id+"F1.opRevolve","SWEPT_BODY",BODY,{"disambiguationData":[OSD([sQuery(id+"F0.wireOp",EDGE,"E1")])]}),"instanceName":"1"}),"instanceName":"1"}),"instanceName":"1"}),"instanceName":"1"}),"instanceName":"1"}),"instanceName":"1"}),"instanceName":"1"});
            var Q2890;
            Q2890=makeQuery(id+"F13.opPattern","COPY",BODY,{"derivedFrom":makeQuery(id+"F12.opPattern","COPY",BODY,{"derivedFrom":makeQuery(id+"F11.opPattern","COPY",BODY,{"derivedFrom":makeQuery(id+"F10.opPattern","COPY",BODY,{"derivedFrom":makeQuery(id+"F5.opPattern","COPY",BODY,{"derivedFrom":makeQuery(id+"F4.opPattern","COPY",BODY,{"derivedFrom":makeQuery(id+"F3.opPattern","COPY",BODY,{"derivedFrom":makeQuery(id+"F2.opPattern","COPY",BODY,{"derivedFrom":makeQuery(id+"F1.opRevolve","SWEPT_BODY",BODY,{"disambiguationData":[OSD([sQuery(id+"F0.wireOp",EDGE,"E1")])]}),"instanceName":"1"}),"instanceName":"1"}),"instanceName":"1"}),"instanceName":"1"}),"instanceName":"1"}),"instanceName":"1"}),"instanceName":"1"}),"instanceName":"1"});
            var Q2891;
            Q2891=makeQuery(id+"F13.opPattern","COPY",BODY,{"derivedFrom":makeQuery(id+"F12.opPattern","COPY",BODY,{"derivedFrom":makeQuery(id+"F11.opPattern","COPY",BODY,{"derivedFrom":makeQuery(id+"F10.opPattern","COPY",BODY,{"derivedFrom":makeQuery(id+"F6.opPattern","COPY",BODY,{"derivedFrom":makeQuery(id+"F1.opRevolve","SWEPT_BODY",BODY,{"disambiguationData":[OSD([sQuery(id+"F0.wireOp",EDGE,"E1")])]}),"instanceName":"1"}),"instanceName":"1"}),"instanceName":"1"}),"instanceName":"1"}),"instanceName":"1"});
            var Q2892;
            Q2892=makeQuery(id+"F13.opPattern","COPY",BODY,{"derivedFrom":makeQuery(id+"F12.opPattern","COPY",BODY,{"derivedFrom":makeQuery(id+"F11.opPattern","COPY",BODY,{"derivedFrom":makeQuery(id+"F10.opPattern","COPY",BODY,{"derivedFrom":makeQuery(id+"F6.opPattern","COPY",BODY,{"derivedFrom":makeQuery(id+"F2.opPattern","COPY",BODY,{"derivedFrom":makeQuery(id+"F1.opRevolve","SWEPT_BODY",BODY,{"disambiguationData":[OSD([sQuery(id+"F0.wireOp",EDGE,"E1")])]}),"instanceName":"1"}),"instanceName":"1"}),"instanceName":"1"}),"instanceName":"1"}),"instanceName":"1"}),"instanceName":"1"});
            var Q2893;
            Q2893=makeQuery(id+"F13.opPattern","COPY",BODY,{"derivedFrom":makeQuery(id+"F12.opPattern","COPY",BODY,{"derivedFrom":makeQuery(id+"F11.opPattern","COPY",BODY,{"derivedFrom":makeQuery(id+"F10.opPattern","COPY",BODY,{"derivedFrom":makeQuery(id+"F6.opPattern","COPY",BODY,{"derivedFrom":makeQuery(id+"F3.opPattern","COPY",BODY,{"derivedFrom":makeQuery(id+"F2.opPattern","COPY",BODY,{"derivedFrom":makeQuery(id+"F1.opRevolve","SWEPT_BODY",BODY,{"disambiguationData":[OSD([sQuery(id+"F0.wireOp",EDGE,"E1")])]}),"instanceName":"1"}),"instanceName":"1"}),"instanceName":"1"}),"instanceName":"1"}),"instanceName":"1"}),"instanceName":"1"}),"instanceName":"1"});
            var Q2894;
            Q2894=makeQuery(id+"F13.opPattern","COPY",BODY,{"derivedFrom":makeQuery(id+"F12.opPattern","COPY",BODY,{"derivedFrom":makeQuery(id+"F11.opPattern","COPY",BODY,{"derivedFrom":makeQuery(id+"F10.opPattern","COPY",BODY,{"derivedFrom":makeQuery(id+"F6.opPattern","COPY",BODY,{"derivedFrom":makeQuery(id+"F4.opPattern","COPY",BODY,{"derivedFrom":makeQuery(id+"F1.opRevolve","SWEPT_BODY",BODY,{"disambiguationData":[OSD([sQuery(id+"F0.wireOp",EDGE,"E1")])]}),"instanceName":"1"}),"instanceName":"1"}),"instanceName":"1"}),"instanceName":"1"}),"instanceName":"1"}),"instanceName":"1"});
            var Q2895;
            Q2895=makeQuery(id+"F13.opPattern","COPY",BODY,{"derivedFrom":makeQuery(id+"F12.opPattern","COPY",BODY,{"derivedFrom":makeQuery(id+"F11.opPattern","COPY",BODY,{"derivedFrom":makeQuery(id+"F10.opPattern","COPY",BODY,{"derivedFrom":makeQuery(id+"F6.opPattern","COPY",BODY,{"derivedFrom":makeQuery(id+"F4.opPattern","COPY",BODY,{"derivedFrom":makeQuery(id+"F2.opPattern","COPY",BODY,{"derivedFrom":makeQuery(id+"F1.opRevolve","SWEPT_BODY",BODY,{"disambiguationData":[OSD([sQuery(id+"F0.wireOp",EDGE,"E1")])]}),"instanceName":"1"}),"instanceName":"1"}),"instanceName":"1"}),"instanceName":"1"}),"instanceName":"1"}),"instanceName":"1"}),"instanceName":"1"});
            var Q2896;
            Q2896=makeQuery(id+"F13.opPattern","COPY",BODY,{"derivedFrom":makeQuery(id+"F12.opPattern","COPY",BODY,{"derivedFrom":makeQuery(id+"F11.opPattern","COPY",BODY,{"derivedFrom":makeQuery(id+"F10.opPattern","COPY",BODY,{"derivedFrom":makeQuery(id+"F6.opPattern","COPY",BODY,{"derivedFrom":makeQuery(id+"F4.opPattern","COPY",BODY,{"derivedFrom":makeQuery(id+"F3.opPattern","COPY",BODY,{"derivedFrom":makeQuery(id+"F2.opPattern","COPY",BODY,{"derivedFrom":makeQuery(id+"F1.opRevolve","SWEPT_BODY",BODY,{"disambiguationData":[OSD([sQuery(id+"F0.wireOp",EDGE,"E1")])]}),"instanceName":"1"}),"instanceName":"1"}),"instanceName":"1"}),"instanceName":"1"}),"instanceName":"1"}),"instanceName":"1"}),"instanceName":"1"}),"instanceName":"1"});
            var Q2897;
            Q2897=makeQuery(id+"F13.opPattern","COPY",BODY,{"derivedFrom":makeQuery(id+"F12.opPattern","COPY",BODY,{"derivedFrom":makeQuery(id+"F11.opPattern","COPY",BODY,{"derivedFrom":makeQuery(id+"F10.opPattern","COPY",BODY,{"derivedFrom":makeQuery(id+"F6.opPattern","COPY",BODY,{"derivedFrom":makeQuery(id+"F5.opPattern","COPY",BODY,{"derivedFrom":makeQuery(id+"F1.opRevolve","SWEPT_BODY",BODY,{"disambiguationData":[OSD([sQuery(id+"F0.wireOp",EDGE,"E1")])]}),"instanceName":"1"}),"instanceName":"1"}),"instanceName":"1"}),"instanceName":"1"}),"instanceName":"1"}),"instanceName":"1"});
            var Q2898;
            Q2898=makeQuery(id+"F13.opPattern","COPY",BODY,{"derivedFrom":makeQuery(id+"F12.opPattern","COPY",BODY,{"derivedFrom":makeQuery(id+"F11.opPattern","COPY",BODY,{"derivedFrom":makeQuery(id+"F10.opPattern","COPY",BODY,{"derivedFrom":makeQuery(id+"F6.opPattern","COPY",BODY,{"derivedFrom":makeQuery(id+"F5.opPattern","COPY",BODY,{"derivedFrom":makeQuery(id+"F2.opPattern","COPY",BODY,{"derivedFrom":makeQuery(id+"F1.opRevolve","SWEPT_BODY",BODY,{"disambiguationData":[OSD([sQuery(id+"F0.wireOp",EDGE,"E1")])]}),"instanceName":"1"}),"instanceName":"1"}),"instanceName":"1"}),"instanceName":"1"}),"instanceName":"1"}),"instanceName":"1"}),"instanceName":"1"});
            var Q2899;
            Q2899=makeQuery(id+"F13.opPattern","COPY",BODY,{"derivedFrom":makeQuery(id+"F12.opPattern","COPY",BODY,{"derivedFrom":makeQuery(id+"F11.opPattern","COPY",BODY,{"derivedFrom":makeQuery(id+"F10.opPattern","COPY",BODY,{"derivedFrom":makeQuery(id+"F6.opPattern","COPY",BODY,{"derivedFrom":makeQuery(id+"F5.opPattern","COPY",BODY,{"derivedFrom":makeQuery(id+"F3.opPattern","COPY",BODY,{"derivedFrom":makeQuery(id+"F2.opPattern","COPY",BODY,{"derivedFrom":makeQuery(id+"F1.opRevolve","SWEPT_BODY",BODY,{"disambiguationData":[OSD([sQuery(id+"F0.wireOp",EDGE,"E1")])]}),"instanceName":"1"}),"instanceName":"1"}),"instanceName":"1"}),"instanceName":"1"}),"instanceName":"1"}),"instanceName":"1"}),"instanceName":"1"}),"instanceName":"1"});
            var Q2900;
            Q2900=makeQuery(id+"F13.opPattern","COPY",BODY,{"derivedFrom":makeQuery(id+"F12.opPattern","COPY",BODY,{"derivedFrom":makeQuery(id+"F11.opPattern","COPY",BODY,{"derivedFrom":makeQuery(id+"F10.opPattern","COPY",BODY,{"derivedFrom":makeQuery(id+"F6.opPattern","COPY",BODY,{"derivedFrom":makeQuery(id+"F5.opPattern","COPY",BODY,{"derivedFrom":makeQuery(id+"F4.opPattern","COPY",BODY,{"derivedFrom":makeQuery(id+"F1.opRevolve","SWEPT_BODY",BODY,{"disambiguationData":[OSD([sQuery(id+"F0.wireOp",EDGE,"E1")])]}),"instanceName":"1"}),"instanceName":"1"}),"instanceName":"1"}),"instanceName":"1"}),"instanceName":"1"}),"instanceName":"1"}),"instanceName":"1"});
            var Q2901;
            Q2901=makeQuery(id+"F13.opPattern","COPY",BODY,{"derivedFrom":makeQuery(id+"F12.opPattern","COPY",BODY,{"derivedFrom":makeQuery(id+"F11.opPattern","COPY",BODY,{"derivedFrom":makeQuery(id+"F10.opPattern","COPY",BODY,{"derivedFrom":makeQuery(id+"F6.opPattern","COPY",BODY,{"derivedFrom":makeQuery(id+"F5.opPattern","COPY",BODY,{"derivedFrom":makeQuery(id+"F4.opPattern","COPY",BODY,{"derivedFrom":makeQuery(id+"F2.opPattern","COPY",BODY,{"derivedFrom":makeQuery(id+"F1.opRevolve","SWEPT_BODY",BODY,{"disambiguationData":[OSD([sQuery(id+"F0.wireOp",EDGE,"E1")])]}),"instanceName":"1"}),"instanceName":"1"}),"instanceName":"1"}),"instanceName":"1"}),"instanceName":"1"}),"instanceName":"1"}),"instanceName":"1"}),"instanceName":"1"});
            var Q2902;
            Q2902=makeQuery(id+"F13.opPattern","COPY",BODY,{"derivedFrom":makeQuery(id+"F12.opPattern","COPY",BODY,{"derivedFrom":makeQuery(id+"F11.opPattern","COPY",BODY,{"derivedFrom":makeQuery(id+"F10.opPattern","COPY",BODY,{"derivedFrom":makeQuery(id+"F6.opPattern","COPY",BODY,{"derivedFrom":makeQuery(id+"F5.opPattern","COPY",BODY,{"derivedFrom":makeQuery(id+"F4.opPattern","COPY",BODY,{"derivedFrom":makeQuery(id+"F3.opPattern","COPY",BODY,{"derivedFrom":makeQuery(id+"F2.opPattern","COPY",BODY,{"derivedFrom":makeQuery(id+"F1.opRevolve","SWEPT_BODY",BODY,{"disambiguationData":[OSD([sQuery(id+"F0.wireOp",EDGE,"E1")])]}),"instanceName":"1"}),"instanceName":"1"}),"instanceName":"1"}),"instanceName":"1"}),"instanceName":"1"}),"instanceName":"1"}),"instanceName":"1"}),"instanceName":"1"}),"instanceName":"1"});
            var Q2903;
            Q2903=makeQuery(id+"F13.opPattern","COPY",BODY,{"derivedFrom":makeQuery(id+"F12.opPattern","COPY",BODY,{"derivedFrom":makeQuery(id+"F11.opPattern","COPY",BODY,{"derivedFrom":makeQuery(id+"F10.opPattern","COPY",BODY,{"derivedFrom":makeQuery(id+"F7.opPattern","COPY",BODY,{"derivedFrom":makeQuery(id+"F1.opRevolve","SWEPT_BODY",BODY,{"disambiguationData":[OSD([sQuery(id+"F0.wireOp",EDGE,"E1")])]}),"instanceName":"1"}),"instanceName":"1"}),"instanceName":"1"}),"instanceName":"1"}),"instanceName":"1"});
            var Q2904;
            Q2904=makeQuery(id+"F13.opPattern","COPY",BODY,{"derivedFrom":makeQuery(id+"F12.opPattern","COPY",BODY,{"derivedFrom":makeQuery(id+"F11.opPattern","COPY",BODY,{"derivedFrom":makeQuery(id+"F10.opPattern","COPY",BODY,{"derivedFrom":makeQuery(id+"F7.opPattern","COPY",BODY,{"derivedFrom":makeQuery(id+"F2.opPattern","COPY",BODY,{"derivedFrom":makeQuery(id+"F1.opRevolve","SWEPT_BODY",BODY,{"disambiguationData":[OSD([sQuery(id+"F0.wireOp",EDGE,"E1")])]}),"instanceName":"1"}),"instanceName":"1"}),"instanceName":"1"}),"instanceName":"1"}),"instanceName":"1"}),"instanceName":"1"});
            var Q2905;
            Q2905=makeQuery(id+"F13.opPattern","COPY",BODY,{"derivedFrom":makeQuery(id+"F12.opPattern","COPY",BODY,{"derivedFrom":makeQuery(id+"F11.opPattern","COPY",BODY,{"derivedFrom":makeQuery(id+"F10.opPattern","COPY",BODY,{"derivedFrom":makeQuery(id+"F7.opPattern","COPY",BODY,{"derivedFrom":makeQuery(id+"F3.opPattern","COPY",BODY,{"derivedFrom":makeQuery(id+"F2.opPattern","COPY",BODY,{"derivedFrom":makeQuery(id+"F1.opRevolve","SWEPT_BODY",BODY,{"disambiguationData":[OSD([sQuery(id+"F0.wireOp",EDGE,"E1")])]}),"instanceName":"1"}),"instanceName":"1"}),"instanceName":"1"}),"instanceName":"1"}),"instanceName":"1"}),"instanceName":"1"}),"instanceName":"1"});
            var Q2906;
            Q2906=makeQuery(id+"F13.opPattern","COPY",BODY,{"derivedFrom":makeQuery(id+"F12.opPattern","COPY",BODY,{"derivedFrom":makeQuery(id+"F11.opPattern","COPY",BODY,{"derivedFrom":makeQuery(id+"F10.opPattern","COPY",BODY,{"derivedFrom":makeQuery(id+"F7.opPattern","COPY",BODY,{"derivedFrom":makeQuery(id+"F4.opPattern","COPY",BODY,{"derivedFrom":makeQuery(id+"F1.opRevolve","SWEPT_BODY",BODY,{"disambiguationData":[OSD([sQuery(id+"F0.wireOp",EDGE,"E1")])]}),"instanceName":"1"}),"instanceName":"1"}),"instanceName":"1"}),"instanceName":"1"}),"instanceName":"1"}),"instanceName":"1"});
            var Q2907;
            Q2907=makeQuery(id+"F13.opPattern","COPY",BODY,{"derivedFrom":makeQuery(id+"F12.opPattern","COPY",BODY,{"derivedFrom":makeQuery(id+"F11.opPattern","COPY",BODY,{"derivedFrom":makeQuery(id+"F10.opPattern","COPY",BODY,{"derivedFrom":makeQuery(id+"F7.opPattern","COPY",BODY,{"derivedFrom":makeQuery(id+"F4.opPattern","COPY",BODY,{"derivedFrom":makeQuery(id+"F2.opPattern","COPY",BODY,{"derivedFrom":makeQuery(id+"F1.opRevolve","SWEPT_BODY",BODY,{"disambiguationData":[OSD([sQuery(id+"F0.wireOp",EDGE,"E1")])]}),"instanceName":"1"}),"instanceName":"1"}),"instanceName":"1"}),"instanceName":"1"}),"instanceName":"1"}),"instanceName":"1"}),"instanceName":"1"});
            var Q2908;
            Q2908=makeQuery(id+"F13.opPattern","COPY",BODY,{"derivedFrom":makeQuery(id+"F12.opPattern","COPY",BODY,{"derivedFrom":makeQuery(id+"F11.opPattern","COPY",BODY,{"derivedFrom":makeQuery(id+"F10.opPattern","COPY",BODY,{"derivedFrom":makeQuery(id+"F7.opPattern","COPY",BODY,{"derivedFrom":makeQuery(id+"F4.opPattern","COPY",BODY,{"derivedFrom":makeQuery(id+"F3.opPattern","COPY",BODY,{"derivedFrom":makeQuery(id+"F2.opPattern","COPY",BODY,{"derivedFrom":makeQuery(id+"F1.opRevolve","SWEPT_BODY",BODY,{"disambiguationData":[OSD([sQuery(id+"F0.wireOp",EDGE,"E1")])]}),"instanceName":"1"}),"instanceName":"1"}),"instanceName":"1"}),"instanceName":"1"}),"instanceName":"1"}),"instanceName":"1"}),"instanceName":"1"}),"instanceName":"1"});
            var Q2909;
            Q2909=makeQuery(id+"F13.opPattern","COPY",BODY,{"derivedFrom":makeQuery(id+"F12.opPattern","COPY",BODY,{"derivedFrom":makeQuery(id+"F11.opPattern","COPY",BODY,{"derivedFrom":makeQuery(id+"F10.opPattern","COPY",BODY,{"derivedFrom":makeQuery(id+"F7.opPattern","COPY",BODY,{"derivedFrom":makeQuery(id+"F5.opPattern","COPY",BODY,{"derivedFrom":makeQuery(id+"F1.opRevolve","SWEPT_BODY",BODY,{"disambiguationData":[OSD([sQuery(id+"F0.wireOp",EDGE,"E1")])]}),"instanceName":"1"}),"instanceName":"1"}),"instanceName":"1"}),"instanceName":"1"}),"instanceName":"1"}),"instanceName":"1"});
            var Q2910;
            Q2910=makeQuery(id+"F13.opPattern","COPY",BODY,{"derivedFrom":makeQuery(id+"F12.opPattern","COPY",BODY,{"derivedFrom":makeQuery(id+"F11.opPattern","COPY",BODY,{"derivedFrom":makeQuery(id+"F10.opPattern","COPY",BODY,{"derivedFrom":makeQuery(id+"F7.opPattern","COPY",BODY,{"derivedFrom":makeQuery(id+"F5.opPattern","COPY",BODY,{"derivedFrom":makeQuery(id+"F2.opPattern","COPY",BODY,{"derivedFrom":makeQuery(id+"F1.opRevolve","SWEPT_BODY",BODY,{"disambiguationData":[OSD([sQuery(id+"F0.wireOp",EDGE,"E1")])]}),"instanceName":"1"}),"instanceName":"1"}),"instanceName":"1"}),"instanceName":"1"}),"instanceName":"1"}),"instanceName":"1"}),"instanceName":"1"});
            var Q2911;
            Q2911=makeQuery(id+"F13.opPattern","COPY",BODY,{"derivedFrom":makeQuery(id+"F12.opPattern","COPY",BODY,{"derivedFrom":makeQuery(id+"F11.opPattern","COPY",BODY,{"derivedFrom":makeQuery(id+"F10.opPattern","COPY",BODY,{"derivedFrom":makeQuery(id+"F7.opPattern","COPY",BODY,{"derivedFrom":makeQuery(id+"F5.opPattern","COPY",BODY,{"derivedFrom":makeQuery(id+"F3.opPattern","COPY",BODY,{"derivedFrom":makeQuery(id+"F2.opPattern","COPY",BODY,{"derivedFrom":makeQuery(id+"F1.opRevolve","SWEPT_BODY",BODY,{"disambiguationData":[OSD([sQuery(id+"F0.wireOp",EDGE,"E1")])]}),"instanceName":"1"}),"instanceName":"1"}),"instanceName":"1"}),"instanceName":"1"}),"instanceName":"1"}),"instanceName":"1"}),"instanceName":"1"}),"instanceName":"1"});
            var Q2912;
            Q2912=makeQuery(id+"F13.opPattern","COPY",BODY,{"derivedFrom":makeQuery(id+"F12.opPattern","COPY",BODY,{"derivedFrom":makeQuery(id+"F11.opPattern","COPY",BODY,{"derivedFrom":makeQuery(id+"F10.opPattern","COPY",BODY,{"derivedFrom":makeQuery(id+"F7.opPattern","COPY",BODY,{"derivedFrom":makeQuery(id+"F5.opPattern","COPY",BODY,{"derivedFrom":makeQuery(id+"F4.opPattern","COPY",BODY,{"derivedFrom":makeQuery(id+"F1.opRevolve","SWEPT_BODY",BODY,{"disambiguationData":[OSD([sQuery(id+"F0.wireOp",EDGE,"E1")])]}),"instanceName":"1"}),"instanceName":"1"}),"instanceName":"1"}),"instanceName":"1"}),"instanceName":"1"}),"instanceName":"1"}),"instanceName":"1"});
            var Q2913;
            Q2913=makeQuery(id+"F13.opPattern","COPY",BODY,{"derivedFrom":makeQuery(id+"F12.opPattern","COPY",BODY,{"derivedFrom":makeQuery(id+"F11.opPattern","COPY",BODY,{"derivedFrom":makeQuery(id+"F10.opPattern","COPY",BODY,{"derivedFrom":makeQuery(id+"F7.opPattern","COPY",BODY,{"derivedFrom":makeQuery(id+"F5.opPattern","COPY",BODY,{"derivedFrom":makeQuery(id+"F4.opPattern","COPY",BODY,{"derivedFrom":makeQuery(id+"F2.opPattern","COPY",BODY,{"derivedFrom":makeQuery(id+"F1.opRevolve","SWEPT_BODY",BODY,{"disambiguationData":[OSD([sQuery(id+"F0.wireOp",EDGE,"E1")])]}),"instanceName":"1"}),"instanceName":"1"}),"instanceName":"1"}),"instanceName":"1"}),"instanceName":"1"}),"instanceName":"1"}),"instanceName":"1"}),"instanceName":"1"});
            var Q2914;
            Q2914=makeQuery(id+"F13.opPattern","COPY",BODY,{"derivedFrom":makeQuery(id+"F12.opPattern","COPY",BODY,{"derivedFrom":makeQuery(id+"F11.opPattern","COPY",BODY,{"derivedFrom":makeQuery(id+"F10.opPattern","COPY",BODY,{"derivedFrom":makeQuery(id+"F7.opPattern","COPY",BODY,{"derivedFrom":makeQuery(id+"F5.opPattern","COPY",BODY,{"derivedFrom":makeQuery(id+"F4.opPattern","COPY",BODY,{"derivedFrom":makeQuery(id+"F3.opPattern","COPY",BODY,{"derivedFrom":makeQuery(id+"F2.opPattern","COPY",BODY,{"derivedFrom":makeQuery(id+"F1.opRevolve","SWEPT_BODY",BODY,{"disambiguationData":[OSD([sQuery(id+"F0.wireOp",EDGE,"E1")])]}),"instanceName":"1"}),"instanceName":"1"}),"instanceName":"1"}),"instanceName":"1"}),"instanceName":"1"}),"instanceName":"1"}),"instanceName":"1"}),"instanceName":"1"}),"instanceName":"1"});
            var Q2915;
            Q2915=makeQuery(id+"F13.opPattern","COPY",BODY,{"derivedFrom":makeQuery(id+"F12.opPattern","COPY",BODY,{"derivedFrom":makeQuery(id+"F11.opPattern","COPY",BODY,{"derivedFrom":makeQuery(id+"F10.opPattern","COPY",BODY,{"derivedFrom":makeQuery(id+"F7.opPattern","COPY",BODY,{"derivedFrom":makeQuery(id+"F6.opPattern","COPY",BODY,{"derivedFrom":makeQuery(id+"F1.opRevolve","SWEPT_BODY",BODY,{"disambiguationData":[OSD([sQuery(id+"F0.wireOp",EDGE,"E1")])]}),"instanceName":"1"}),"instanceName":"1"}),"instanceName":"1"}),"instanceName":"1"}),"instanceName":"1"}),"instanceName":"1"});
            var Q2916;
            Q2916=makeQuery(id+"F13.opPattern","COPY",BODY,{"derivedFrom":makeQuery(id+"F12.opPattern","COPY",BODY,{"derivedFrom":makeQuery(id+"F11.opPattern","COPY",BODY,{"derivedFrom":makeQuery(id+"F10.opPattern","COPY",BODY,{"derivedFrom":makeQuery(id+"F7.opPattern","COPY",BODY,{"derivedFrom":makeQuery(id+"F6.opPattern","COPY",BODY,{"derivedFrom":makeQuery(id+"F2.opPattern","COPY",BODY,{"derivedFrom":makeQuery(id+"F1.opRevolve","SWEPT_BODY",BODY,{"disambiguationData":[OSD([sQuery(id+"F0.wireOp",EDGE,"E1")])]}),"instanceName":"1"}),"instanceName":"1"}),"instanceName":"1"}),"instanceName":"1"}),"instanceName":"1"}),"instanceName":"1"}),"instanceName":"1"});
            var Q2917;
            Q2917=makeQuery(id+"F13.opPattern","COPY",BODY,{"derivedFrom":makeQuery(id+"F12.opPattern","COPY",BODY,{"derivedFrom":makeQuery(id+"F11.opPattern","COPY",BODY,{"derivedFrom":makeQuery(id+"F10.opPattern","COPY",BODY,{"derivedFrom":makeQuery(id+"F7.opPattern","COPY",BODY,{"derivedFrom":makeQuery(id+"F6.opPattern","COPY",BODY,{"derivedFrom":makeQuery(id+"F3.opPattern","COPY",BODY,{"derivedFrom":makeQuery(id+"F2.opPattern","COPY",BODY,{"derivedFrom":makeQuery(id+"F1.opRevolve","SWEPT_BODY",BODY,{"disambiguationData":[OSD([sQuery(id+"F0.wireOp",EDGE,"E1")])]}),"instanceName":"1"}),"instanceName":"1"}),"instanceName":"1"}),"instanceName":"1"}),"instanceName":"1"}),"instanceName":"1"}),"instanceName":"1"}),"instanceName":"1"});
            var Q2918;
            Q2918=makeQuery(id+"F13.opPattern","COPY",BODY,{"derivedFrom":makeQuery(id+"F12.opPattern","COPY",BODY,{"derivedFrom":makeQuery(id+"F11.opPattern","COPY",BODY,{"derivedFrom":makeQuery(id+"F10.opPattern","COPY",BODY,{"derivedFrom":makeQuery(id+"F7.opPattern","COPY",BODY,{"derivedFrom":makeQuery(id+"F6.opPattern","COPY",BODY,{"derivedFrom":makeQuery(id+"F4.opPattern","COPY",BODY,{"derivedFrom":makeQuery(id+"F1.opRevolve","SWEPT_BODY",BODY,{"disambiguationData":[OSD([sQuery(id+"F0.wireOp",EDGE,"E1")])]}),"instanceName":"1"}),"instanceName":"1"}),"instanceName":"1"}),"instanceName":"1"}),"instanceName":"1"}),"instanceName":"1"}),"instanceName":"1"});
            var Q2919;
            Q2919=makeQuery(id+"F13.opPattern","COPY",BODY,{"derivedFrom":makeQuery(id+"F12.opPattern","COPY",BODY,{"derivedFrom":makeQuery(id+"F11.opPattern","COPY",BODY,{"derivedFrom":makeQuery(id+"F10.opPattern","COPY",BODY,{"derivedFrom":makeQuery(id+"F7.opPattern","COPY",BODY,{"derivedFrom":makeQuery(id+"F6.opPattern","COPY",BODY,{"derivedFrom":makeQuery(id+"F4.opPattern","COPY",BODY,{"derivedFrom":makeQuery(id+"F2.opPattern","COPY",BODY,{"derivedFrom":makeQuery(id+"F1.opRevolve","SWEPT_BODY",BODY,{"disambiguationData":[OSD([sQuery(id+"F0.wireOp",EDGE,"E1")])]}),"instanceName":"1"}),"instanceName":"1"}),"instanceName":"1"}),"instanceName":"1"}),"instanceName":"1"}),"instanceName":"1"}),"instanceName":"1"}),"instanceName":"1"});
            var Q2920;
            Q2920=makeQuery(id+"F13.opPattern","COPY",BODY,{"derivedFrom":makeQuery(id+"F12.opPattern","COPY",BODY,{"derivedFrom":makeQuery(id+"F11.opPattern","COPY",BODY,{"derivedFrom":makeQuery(id+"F10.opPattern","COPY",BODY,{"derivedFrom":makeQuery(id+"F7.opPattern","COPY",BODY,{"derivedFrom":makeQuery(id+"F6.opPattern","COPY",BODY,{"derivedFrom":makeQuery(id+"F4.opPattern","COPY",BODY,{"derivedFrom":makeQuery(id+"F3.opPattern","COPY",BODY,{"derivedFrom":makeQuery(id+"F2.opPattern","COPY",BODY,{"derivedFrom":makeQuery(id+"F1.opRevolve","SWEPT_BODY",BODY,{"disambiguationData":[OSD([sQuery(id+"F0.wireOp",EDGE,"E1")])]}),"instanceName":"1"}),"instanceName":"1"}),"instanceName":"1"}),"instanceName":"1"}),"instanceName":"1"}),"instanceName":"1"}),"instanceName":"1"}),"instanceName":"1"}),"instanceName":"1"});
            var Q2921;
            Q2921=makeQuery(id+"F13.opPattern","COPY",BODY,{"derivedFrom":makeQuery(id+"F12.opPattern","COPY",BODY,{"derivedFrom":makeQuery(id+"F11.opPattern","COPY",BODY,{"derivedFrom":makeQuery(id+"F10.opPattern","COPY",BODY,{"derivedFrom":makeQuery(id+"F7.opPattern","COPY",BODY,{"derivedFrom":makeQuery(id+"F6.opPattern","COPY",BODY,{"derivedFrom":makeQuery(id+"F5.opPattern","COPY",BODY,{"derivedFrom":makeQuery(id+"F1.opRevolve","SWEPT_BODY",BODY,{"disambiguationData":[OSD([sQuery(id+"F0.wireOp",EDGE,"E1")])]}),"instanceName":"1"}),"instanceName":"1"}),"instanceName":"1"}),"instanceName":"1"}),"instanceName":"1"}),"instanceName":"1"}),"instanceName":"1"});
            var Q2922;
            Q2922=makeQuery(id+"F13.opPattern","COPY",BODY,{"derivedFrom":makeQuery(id+"F12.opPattern","COPY",BODY,{"derivedFrom":makeQuery(id+"F11.opPattern","COPY",BODY,{"derivedFrom":makeQuery(id+"F10.opPattern","COPY",BODY,{"derivedFrom":makeQuery(id+"F7.opPattern","COPY",BODY,{"derivedFrom":makeQuery(id+"F6.opPattern","COPY",BODY,{"derivedFrom":makeQuery(id+"F5.opPattern","COPY",BODY,{"derivedFrom":makeQuery(id+"F2.opPattern","COPY",BODY,{"derivedFrom":makeQuery(id+"F1.opRevolve","SWEPT_BODY",BODY,{"disambiguationData":[OSD([sQuery(id+"F0.wireOp",EDGE,"E1")])]}),"instanceName":"1"}),"instanceName":"1"}),"instanceName":"1"}),"instanceName":"1"}),"instanceName":"1"}),"instanceName":"1"}),"instanceName":"1"}),"instanceName":"1"});
            var Q2923;
            Q2923=makeQuery(id+"F13.opPattern","COPY",BODY,{"derivedFrom":makeQuery(id+"F12.opPattern","COPY",BODY,{"derivedFrom":makeQuery(id+"F11.opPattern","COPY",BODY,{"derivedFrom":makeQuery(id+"F10.opPattern","COPY",BODY,{"derivedFrom":makeQuery(id+"F7.opPattern","COPY",BODY,{"derivedFrom":makeQuery(id+"F6.opPattern","COPY",BODY,{"derivedFrom":makeQuery(id+"F5.opPattern","COPY",BODY,{"derivedFrom":makeQuery(id+"F3.opPattern","COPY",BODY,{"derivedFrom":makeQuery(id+"F2.opPattern","COPY",BODY,{"derivedFrom":makeQuery(id+"F1.opRevolve","SWEPT_BODY",BODY,{"disambiguationData":[OSD([sQuery(id+"F0.wireOp",EDGE,"E1")])]}),"instanceName":"1"}),"instanceName":"1"}),"instanceName":"1"}),"instanceName":"1"}),"instanceName":"1"}),"instanceName":"1"}),"instanceName":"1"}),"instanceName":"1"}),"instanceName":"1"});
            var Q2924;
            Q2924=makeQuery(id+"F13.opPattern","COPY",BODY,{"derivedFrom":makeQuery(id+"F12.opPattern","COPY",BODY,{"derivedFrom":makeQuery(id+"F11.opPattern","COPY",BODY,{"derivedFrom":makeQuery(id+"F10.opPattern","COPY",BODY,{"derivedFrom":makeQuery(id+"F7.opPattern","COPY",BODY,{"derivedFrom":makeQuery(id+"F6.opPattern","COPY",BODY,{"derivedFrom":makeQuery(id+"F5.opPattern","COPY",BODY,{"derivedFrom":makeQuery(id+"F4.opPattern","COPY",BODY,{"derivedFrom":makeQuery(id+"F1.opRevolve","SWEPT_BODY",BODY,{"disambiguationData":[OSD([sQuery(id+"F0.wireOp",EDGE,"E1")])]}),"instanceName":"1"}),"instanceName":"1"}),"instanceName":"1"}),"instanceName":"1"}),"instanceName":"1"}),"instanceName":"1"}),"instanceName":"1"}),"instanceName":"1"});
            var Q2925;
            Q2925=makeQuery(id+"F13.opPattern","COPY",BODY,{"derivedFrom":makeQuery(id+"F12.opPattern","COPY",BODY,{"derivedFrom":makeQuery(id+"F11.opPattern","COPY",BODY,{"derivedFrom":makeQuery(id+"F10.opPattern","COPY",BODY,{"derivedFrom":makeQuery(id+"F7.opPattern","COPY",BODY,{"derivedFrom":makeQuery(id+"F6.opPattern","COPY",BODY,{"derivedFrom":makeQuery(id+"F5.opPattern","COPY",BODY,{"derivedFrom":makeQuery(id+"F4.opPattern","COPY",BODY,{"derivedFrom":makeQuery(id+"F2.opPattern","COPY",BODY,{"derivedFrom":makeQuery(id+"F1.opRevolve","SWEPT_BODY",BODY,{"disambiguationData":[OSD([sQuery(id+"F0.wireOp",EDGE,"E1")])]}),"instanceName":"1"}),"instanceName":"1"}),"instanceName":"1"}),"instanceName":"1"}),"instanceName":"1"}),"instanceName":"1"}),"instanceName":"1"}),"instanceName":"1"}),"instanceName":"1"});
            var Q2926;
            Q2926=makeQuery(id+"F13.opPattern","COPY",BODY,{"derivedFrom":makeQuery(id+"F12.opPattern","COPY",BODY,{"derivedFrom":makeQuery(id+"F11.opPattern","COPY",BODY,{"derivedFrom":makeQuery(id+"F10.opPattern","COPY",BODY,{"derivedFrom":makeQuery(id+"F7.opPattern","COPY",BODY,{"derivedFrom":makeQuery(id+"F6.opPattern","COPY",BODY,{"derivedFrom":makeQuery(id+"F5.opPattern","COPY",BODY,{"derivedFrom":makeQuery(id+"F4.opPattern","COPY",BODY,{"derivedFrom":makeQuery(id+"F3.opPattern","COPY",BODY,{"derivedFrom":makeQuery(id+"F2.opPattern","COPY",BODY,{"derivedFrom":makeQuery(id+"F1.opRevolve","SWEPT_BODY",BODY,{"disambiguationData":[OSD([sQuery(id+"F0.wireOp",EDGE,"E1")])]}),"instanceName":"1"}),"instanceName":"1"}),"instanceName":"1"}),"instanceName":"1"}),"instanceName":"1"}),"instanceName":"1"}),"instanceName":"1"}),"instanceName":"1"}),"instanceName":"1"}),"instanceName":"1"});
            var Q2927;
            Q2927=makeQuery(id+"F13.opPattern","COPY",BODY,{"derivedFrom":makeQuery(id+"F12.opPattern","COPY",BODY,{"derivedFrom":makeQuery(id+"F11.opPattern","COPY",BODY,{"derivedFrom":makeQuery(id+"F10.opPattern","COPY",BODY,{"derivedFrom":makeQuery(id+"F8.opPattern","COPY",BODY,{"derivedFrom":makeQuery(id+"F1.opRevolve","SWEPT_BODY",BODY,{"disambiguationData":[OSD([sQuery(id+"F0.wireOp",EDGE,"E1")])]}),"instanceName":"1"}),"instanceName":"1"}),"instanceName":"1"}),"instanceName":"1"}),"instanceName":"1"});
            var Q2928;
            Q2928=makeQuery(id+"F13.opPattern","COPY",BODY,{"derivedFrom":makeQuery(id+"F12.opPattern","COPY",BODY,{"derivedFrom":makeQuery(id+"F11.opPattern","COPY",BODY,{"derivedFrom":makeQuery(id+"F10.opPattern","COPY",BODY,{"derivedFrom":makeQuery(id+"F8.opPattern","COPY",BODY,{"derivedFrom":makeQuery(id+"F2.opPattern","COPY",BODY,{"derivedFrom":makeQuery(id+"F1.opRevolve","SWEPT_BODY",BODY,{"disambiguationData":[OSD([sQuery(id+"F0.wireOp",EDGE,"E1")])]}),"instanceName":"1"}),"instanceName":"1"}),"instanceName":"1"}),"instanceName":"1"}),"instanceName":"1"}),"instanceName":"1"});
            var Q2929;
            Q2929=makeQuery(id+"F13.opPattern","COPY",BODY,{"derivedFrom":makeQuery(id+"F12.opPattern","COPY",BODY,{"derivedFrom":makeQuery(id+"F11.opPattern","COPY",BODY,{"derivedFrom":makeQuery(id+"F10.opPattern","COPY",BODY,{"derivedFrom":makeQuery(id+"F8.opPattern","COPY",BODY,{"derivedFrom":makeQuery(id+"F3.opPattern","COPY",BODY,{"derivedFrom":makeQuery(id+"F2.opPattern","COPY",BODY,{"derivedFrom":makeQuery(id+"F1.opRevolve","SWEPT_BODY",BODY,{"disambiguationData":[OSD([sQuery(id+"F0.wireOp",EDGE,"E1")])]}),"instanceName":"1"}),"instanceName":"1"}),"instanceName":"1"}),"instanceName":"1"}),"instanceName":"1"}),"instanceName":"1"}),"instanceName":"1"});
            var Q2930;
            Q2930=makeQuery(id+"F13.opPattern","COPY",BODY,{"derivedFrom":makeQuery(id+"F12.opPattern","COPY",BODY,{"derivedFrom":makeQuery(id+"F11.opPattern","COPY",BODY,{"derivedFrom":makeQuery(id+"F10.opPattern","COPY",BODY,{"derivedFrom":makeQuery(id+"F8.opPattern","COPY",BODY,{"derivedFrom":makeQuery(id+"F4.opPattern","COPY",BODY,{"derivedFrom":makeQuery(id+"F1.opRevolve","SWEPT_BODY",BODY,{"disambiguationData":[OSD([sQuery(id+"F0.wireOp",EDGE,"E1")])]}),"instanceName":"1"}),"instanceName":"1"}),"instanceName":"1"}),"instanceName":"1"}),"instanceName":"1"}),"instanceName":"1"});
            var Q2931;
            Q2931=makeQuery(id+"F13.opPattern","COPY",BODY,{"derivedFrom":makeQuery(id+"F12.opPattern","COPY",BODY,{"derivedFrom":makeQuery(id+"F11.opPattern","COPY",BODY,{"derivedFrom":makeQuery(id+"F10.opPattern","COPY",BODY,{"derivedFrom":makeQuery(id+"F8.opPattern","COPY",BODY,{"derivedFrom":makeQuery(id+"F4.opPattern","COPY",BODY,{"derivedFrom":makeQuery(id+"F2.opPattern","COPY",BODY,{"derivedFrom":makeQuery(id+"F1.opRevolve","SWEPT_BODY",BODY,{"disambiguationData":[OSD([sQuery(id+"F0.wireOp",EDGE,"E1")])]}),"instanceName":"1"}),"instanceName":"1"}),"instanceName":"1"}),"instanceName":"1"}),"instanceName":"1"}),"instanceName":"1"}),"instanceName":"1"});
            var Q2932;
            Q2932=makeQuery(id+"F13.opPattern","COPY",BODY,{"derivedFrom":makeQuery(id+"F12.opPattern","COPY",BODY,{"derivedFrom":makeQuery(id+"F11.opPattern","COPY",BODY,{"derivedFrom":makeQuery(id+"F10.opPattern","COPY",BODY,{"derivedFrom":makeQuery(id+"F8.opPattern","COPY",BODY,{"derivedFrom":makeQuery(id+"F4.opPattern","COPY",BODY,{"derivedFrom":makeQuery(id+"F3.opPattern","COPY",BODY,{"derivedFrom":makeQuery(id+"F2.opPattern","COPY",BODY,{"derivedFrom":makeQuery(id+"F1.opRevolve","SWEPT_BODY",BODY,{"disambiguationData":[OSD([sQuery(id+"F0.wireOp",EDGE,"E1")])]}),"instanceName":"1"}),"instanceName":"1"}),"instanceName":"1"}),"instanceName":"1"}),"instanceName":"1"}),"instanceName":"1"}),"instanceName":"1"}),"instanceName":"1"});
            var Q2933;
            Q2933=makeQuery(id+"F13.opPattern","COPY",BODY,{"derivedFrom":makeQuery(id+"F12.opPattern","COPY",BODY,{"derivedFrom":makeQuery(id+"F11.opPattern","COPY",BODY,{"derivedFrom":makeQuery(id+"F10.opPattern","COPY",BODY,{"derivedFrom":makeQuery(id+"F8.opPattern","COPY",BODY,{"derivedFrom":makeQuery(id+"F5.opPattern","COPY",BODY,{"derivedFrom":makeQuery(id+"F1.opRevolve","SWEPT_BODY",BODY,{"disambiguationData":[OSD([sQuery(id+"F0.wireOp",EDGE,"E1")])]}),"instanceName":"1"}),"instanceName":"1"}),"instanceName":"1"}),"instanceName":"1"}),"instanceName":"1"}),"instanceName":"1"});
            var Q2934;
            Q2934=makeQuery(id+"F13.opPattern","COPY",BODY,{"derivedFrom":makeQuery(id+"F12.opPattern","COPY",BODY,{"derivedFrom":makeQuery(id+"F11.opPattern","COPY",BODY,{"derivedFrom":makeQuery(id+"F10.opPattern","COPY",BODY,{"derivedFrom":makeQuery(id+"F8.opPattern","COPY",BODY,{"derivedFrom":makeQuery(id+"F5.opPattern","COPY",BODY,{"derivedFrom":makeQuery(id+"F2.opPattern","COPY",BODY,{"derivedFrom":makeQuery(id+"F1.opRevolve","SWEPT_BODY",BODY,{"disambiguationData":[OSD([sQuery(id+"F0.wireOp",EDGE,"E1")])]}),"instanceName":"1"}),"instanceName":"1"}),"instanceName":"1"}),"instanceName":"1"}),"instanceName":"1"}),"instanceName":"1"}),"instanceName":"1"});
            var Q2935;
            Q2935=makeQuery(id+"F13.opPattern","COPY",BODY,{"derivedFrom":makeQuery(id+"F12.opPattern","COPY",BODY,{"derivedFrom":makeQuery(id+"F11.opPattern","COPY",BODY,{"derivedFrom":makeQuery(id+"F10.opPattern","COPY",BODY,{"derivedFrom":makeQuery(id+"F8.opPattern","COPY",BODY,{"derivedFrom":makeQuery(id+"F5.opPattern","COPY",BODY,{"derivedFrom":makeQuery(id+"F3.opPattern","COPY",BODY,{"derivedFrom":makeQuery(id+"F2.opPattern","COPY",BODY,{"derivedFrom":makeQuery(id+"F1.opRevolve","SWEPT_BODY",BODY,{"disambiguationData":[OSD([sQuery(id+"F0.wireOp",EDGE,"E1")])]}),"instanceName":"1"}),"instanceName":"1"}),"instanceName":"1"}),"instanceName":"1"}),"instanceName":"1"}),"instanceName":"1"}),"instanceName":"1"}),"instanceName":"1"});
            var Q2936;
            Q2936=makeQuery(id+"F13.opPattern","COPY",BODY,{"derivedFrom":makeQuery(id+"F12.opPattern","COPY",BODY,{"derivedFrom":makeQuery(id+"F11.opPattern","COPY",BODY,{"derivedFrom":makeQuery(id+"F10.opPattern","COPY",BODY,{"derivedFrom":makeQuery(id+"F8.opPattern","COPY",BODY,{"derivedFrom":makeQuery(id+"F5.opPattern","COPY",BODY,{"derivedFrom":makeQuery(id+"F4.opPattern","COPY",BODY,{"derivedFrom":makeQuery(id+"F1.opRevolve","SWEPT_BODY",BODY,{"disambiguationData":[OSD([sQuery(id+"F0.wireOp",EDGE,"E1")])]}),"instanceName":"1"}),"instanceName":"1"}),"instanceName":"1"}),"instanceName":"1"}),"instanceName":"1"}),"instanceName":"1"}),"instanceName":"1"});
            var Q2937;
            Q2937=makeQuery(id+"F13.opPattern","COPY",BODY,{"derivedFrom":makeQuery(id+"F12.opPattern","COPY",BODY,{"derivedFrom":makeQuery(id+"F11.opPattern","COPY",BODY,{"derivedFrom":makeQuery(id+"F10.opPattern","COPY",BODY,{"derivedFrom":makeQuery(id+"F8.opPattern","COPY",BODY,{"derivedFrom":makeQuery(id+"F5.opPattern","COPY",BODY,{"derivedFrom":makeQuery(id+"F4.opPattern","COPY",BODY,{"derivedFrom":makeQuery(id+"F2.opPattern","COPY",BODY,{"derivedFrom":makeQuery(id+"F1.opRevolve","SWEPT_BODY",BODY,{"disambiguationData":[OSD([sQuery(id+"F0.wireOp",EDGE,"E1")])]}),"instanceName":"1"}),"instanceName":"1"}),"instanceName":"1"}),"instanceName":"1"}),"instanceName":"1"}),"instanceName":"1"}),"instanceName":"1"}),"instanceName":"1"});
            var Q2938;
            Q2938=makeQuery(id+"F13.opPattern","COPY",BODY,{"derivedFrom":makeQuery(id+"F12.opPattern","COPY",BODY,{"derivedFrom":makeQuery(id+"F11.opPattern","COPY",BODY,{"derivedFrom":makeQuery(id+"F10.opPattern","COPY",BODY,{"derivedFrom":makeQuery(id+"F8.opPattern","COPY",BODY,{"derivedFrom":makeQuery(id+"F5.opPattern","COPY",BODY,{"derivedFrom":makeQuery(id+"F4.opPattern","COPY",BODY,{"derivedFrom":makeQuery(id+"F3.opPattern","COPY",BODY,{"derivedFrom":makeQuery(id+"F2.opPattern","COPY",BODY,{"derivedFrom":makeQuery(id+"F1.opRevolve","SWEPT_BODY",BODY,{"disambiguationData":[OSD([sQuery(id+"F0.wireOp",EDGE,"E1")])]}),"instanceName":"1"}),"instanceName":"1"}),"instanceName":"1"}),"instanceName":"1"}),"instanceName":"1"}),"instanceName":"1"}),"instanceName":"1"}),"instanceName":"1"}),"instanceName":"1"});
            var Q2939;
            Q2939=makeQuery(id+"F13.opPattern","COPY",BODY,{"derivedFrom":makeQuery(id+"F12.opPattern","COPY",BODY,{"derivedFrom":makeQuery(id+"F11.opPattern","COPY",BODY,{"derivedFrom":makeQuery(id+"F10.opPattern","COPY",BODY,{"derivedFrom":makeQuery(id+"F8.opPattern","COPY",BODY,{"derivedFrom":makeQuery(id+"F6.opPattern","COPY",BODY,{"derivedFrom":makeQuery(id+"F1.opRevolve","SWEPT_BODY",BODY,{"disambiguationData":[OSD([sQuery(id+"F0.wireOp",EDGE,"E1")])]}),"instanceName":"1"}),"instanceName":"1"}),"instanceName":"1"}),"instanceName":"1"}),"instanceName":"1"}),"instanceName":"1"});
            var Q2940;
            Q2940=makeQuery(id+"F13.opPattern","COPY",BODY,{"derivedFrom":makeQuery(id+"F12.opPattern","COPY",BODY,{"derivedFrom":makeQuery(id+"F11.opPattern","COPY",BODY,{"derivedFrom":makeQuery(id+"F10.opPattern","COPY",BODY,{"derivedFrom":makeQuery(id+"F8.opPattern","COPY",BODY,{"derivedFrom":makeQuery(id+"F6.opPattern","COPY",BODY,{"derivedFrom":makeQuery(id+"F2.opPattern","COPY",BODY,{"derivedFrom":makeQuery(id+"F1.opRevolve","SWEPT_BODY",BODY,{"disambiguationData":[OSD([sQuery(id+"F0.wireOp",EDGE,"E1")])]}),"instanceName":"1"}),"instanceName":"1"}),"instanceName":"1"}),"instanceName":"1"}),"instanceName":"1"}),"instanceName":"1"}),"instanceName":"1"});
            var Q2941;
            Q2941=makeQuery(id+"F13.opPattern","COPY",BODY,{"derivedFrom":makeQuery(id+"F12.opPattern","COPY",BODY,{"derivedFrom":makeQuery(id+"F11.opPattern","COPY",BODY,{"derivedFrom":makeQuery(id+"F10.opPattern","COPY",BODY,{"derivedFrom":makeQuery(id+"F8.opPattern","COPY",BODY,{"derivedFrom":makeQuery(id+"F6.opPattern","COPY",BODY,{"derivedFrom":makeQuery(id+"F3.opPattern","COPY",BODY,{"derivedFrom":makeQuery(id+"F2.opPattern","COPY",BODY,{"derivedFrom":makeQuery(id+"F1.opRevolve","SWEPT_BODY",BODY,{"disambiguationData":[OSD([sQuery(id+"F0.wireOp",EDGE,"E1")])]}),"instanceName":"1"}),"instanceName":"1"}),"instanceName":"1"}),"instanceName":"1"}),"instanceName":"1"}),"instanceName":"1"}),"instanceName":"1"}),"instanceName":"1"});
            var Q2942;
            Q2942=makeQuery(id+"F13.opPattern","COPY",BODY,{"derivedFrom":makeQuery(id+"F12.opPattern","COPY",BODY,{"derivedFrom":makeQuery(id+"F11.opPattern","COPY",BODY,{"derivedFrom":makeQuery(id+"F10.opPattern","COPY",BODY,{"derivedFrom":makeQuery(id+"F8.opPattern","COPY",BODY,{"derivedFrom":makeQuery(id+"F6.opPattern","COPY",BODY,{"derivedFrom":makeQuery(id+"F4.opPattern","COPY",BODY,{"derivedFrom":makeQuery(id+"F1.opRevolve","SWEPT_BODY",BODY,{"disambiguationData":[OSD([sQuery(id+"F0.wireOp",EDGE,"E1")])]}),"instanceName":"1"}),"instanceName":"1"}),"instanceName":"1"}),"instanceName":"1"}),"instanceName":"1"}),"instanceName":"1"}),"instanceName":"1"});
            var Q2943;
            Q2943=makeQuery(id+"F13.opPattern","COPY",BODY,{"derivedFrom":makeQuery(id+"F12.opPattern","COPY",BODY,{"derivedFrom":makeQuery(id+"F11.opPattern","COPY",BODY,{"derivedFrom":makeQuery(id+"F10.opPattern","COPY",BODY,{"derivedFrom":makeQuery(id+"F8.opPattern","COPY",BODY,{"derivedFrom":makeQuery(id+"F6.opPattern","COPY",BODY,{"derivedFrom":makeQuery(id+"F4.opPattern","COPY",BODY,{"derivedFrom":makeQuery(id+"F2.opPattern","COPY",BODY,{"derivedFrom":makeQuery(id+"F1.opRevolve","SWEPT_BODY",BODY,{"disambiguationData":[OSD([sQuery(id+"F0.wireOp",EDGE,"E1")])]}),"instanceName":"1"}),"instanceName":"1"}),"instanceName":"1"}),"instanceName":"1"}),"instanceName":"1"}),"instanceName":"1"}),"instanceName":"1"}),"instanceName":"1"});
            var Q2944;
            Q2944=makeQuery(id+"F13.opPattern","COPY",BODY,{"derivedFrom":makeQuery(id+"F12.opPattern","COPY",BODY,{"derivedFrom":makeQuery(id+"F11.opPattern","COPY",BODY,{"derivedFrom":makeQuery(id+"F10.opPattern","COPY",BODY,{"derivedFrom":makeQuery(id+"F8.opPattern","COPY",BODY,{"derivedFrom":makeQuery(id+"F6.opPattern","COPY",BODY,{"derivedFrom":makeQuery(id+"F4.opPattern","COPY",BODY,{"derivedFrom":makeQuery(id+"F3.opPattern","COPY",BODY,{"derivedFrom":makeQuery(id+"F2.opPattern","COPY",BODY,{"derivedFrom":makeQuery(id+"F1.opRevolve","SWEPT_BODY",BODY,{"disambiguationData":[OSD([sQuery(id+"F0.wireOp",EDGE,"E1")])]}),"instanceName":"1"}),"instanceName":"1"}),"instanceName":"1"}),"instanceName":"1"}),"instanceName":"1"}),"instanceName":"1"}),"instanceName":"1"}),"instanceName":"1"}),"instanceName":"1"});
            var Q2945;
            Q2945=makeQuery(id+"F13.opPattern","COPY",BODY,{"derivedFrom":makeQuery(id+"F12.opPattern","COPY",BODY,{"derivedFrom":makeQuery(id+"F11.opPattern","COPY",BODY,{"derivedFrom":makeQuery(id+"F10.opPattern","COPY",BODY,{"derivedFrom":makeQuery(id+"F8.opPattern","COPY",BODY,{"derivedFrom":makeQuery(id+"F6.opPattern","COPY",BODY,{"derivedFrom":makeQuery(id+"F5.opPattern","COPY",BODY,{"derivedFrom":makeQuery(id+"F1.opRevolve","SWEPT_BODY",BODY,{"disambiguationData":[OSD([sQuery(id+"F0.wireOp",EDGE,"E1")])]}),"instanceName":"1"}),"instanceName":"1"}),"instanceName":"1"}),"instanceName":"1"}),"instanceName":"1"}),"instanceName":"1"}),"instanceName":"1"});
            var Q2946;
            Q2946=makeQuery(id+"F13.opPattern","COPY",BODY,{"derivedFrom":makeQuery(id+"F12.opPattern","COPY",BODY,{"derivedFrom":makeQuery(id+"F11.opPattern","COPY",BODY,{"derivedFrom":makeQuery(id+"F10.opPattern","COPY",BODY,{"derivedFrom":makeQuery(id+"F8.opPattern","COPY",BODY,{"derivedFrom":makeQuery(id+"F6.opPattern","COPY",BODY,{"derivedFrom":makeQuery(id+"F5.opPattern","COPY",BODY,{"derivedFrom":makeQuery(id+"F2.opPattern","COPY",BODY,{"derivedFrom":makeQuery(id+"F1.opRevolve","SWEPT_BODY",BODY,{"disambiguationData":[OSD([sQuery(id+"F0.wireOp",EDGE,"E1")])]}),"instanceName":"1"}),"instanceName":"1"}),"instanceName":"1"}),"instanceName":"1"}),"instanceName":"1"}),"instanceName":"1"}),"instanceName":"1"}),"instanceName":"1"});
            var Q2947;
            Q2947=makeQuery(id+"F13.opPattern","COPY",BODY,{"derivedFrom":makeQuery(id+"F12.opPattern","COPY",BODY,{"derivedFrom":makeQuery(id+"F11.opPattern","COPY",BODY,{"derivedFrom":makeQuery(id+"F10.opPattern","COPY",BODY,{"derivedFrom":makeQuery(id+"F8.opPattern","COPY",BODY,{"derivedFrom":makeQuery(id+"F6.opPattern","COPY",BODY,{"derivedFrom":makeQuery(id+"F5.opPattern","COPY",BODY,{"derivedFrom":makeQuery(id+"F3.opPattern","COPY",BODY,{"derivedFrom":makeQuery(id+"F2.opPattern","COPY",BODY,{"derivedFrom":makeQuery(id+"F1.opRevolve","SWEPT_BODY",BODY,{"disambiguationData":[OSD([sQuery(id+"F0.wireOp",EDGE,"E1")])]}),"instanceName":"1"}),"instanceName":"1"}),"instanceName":"1"}),"instanceName":"1"}),"instanceName":"1"}),"instanceName":"1"}),"instanceName":"1"}),"instanceName":"1"}),"instanceName":"1"});
            var Q2948;
            Q2948=makeQuery(id+"F13.opPattern","COPY",BODY,{"derivedFrom":makeQuery(id+"F12.opPattern","COPY",BODY,{"derivedFrom":makeQuery(id+"F11.opPattern","COPY",BODY,{"derivedFrom":makeQuery(id+"F10.opPattern","COPY",BODY,{"derivedFrom":makeQuery(id+"F8.opPattern","COPY",BODY,{"derivedFrom":makeQuery(id+"F6.opPattern","COPY",BODY,{"derivedFrom":makeQuery(id+"F5.opPattern","COPY",BODY,{"derivedFrom":makeQuery(id+"F4.opPattern","COPY",BODY,{"derivedFrom":makeQuery(id+"F1.opRevolve","SWEPT_BODY",BODY,{"disambiguationData":[OSD([sQuery(id+"F0.wireOp",EDGE,"E1")])]}),"instanceName":"1"}),"instanceName":"1"}),"instanceName":"1"}),"instanceName":"1"}),"instanceName":"1"}),"instanceName":"1"}),"instanceName":"1"}),"instanceName":"1"});
            var Q2949;
            Q2949=makeQuery(id+"F13.opPattern","COPY",BODY,{"derivedFrom":makeQuery(id+"F12.opPattern","COPY",BODY,{"derivedFrom":makeQuery(id+"F11.opPattern","COPY",BODY,{"derivedFrom":makeQuery(id+"F10.opPattern","COPY",BODY,{"derivedFrom":makeQuery(id+"F8.opPattern","COPY",BODY,{"derivedFrom":makeQuery(id+"F6.opPattern","COPY",BODY,{"derivedFrom":makeQuery(id+"F5.opPattern","COPY",BODY,{"derivedFrom":makeQuery(id+"F4.opPattern","COPY",BODY,{"derivedFrom":makeQuery(id+"F2.opPattern","COPY",BODY,{"derivedFrom":makeQuery(id+"F1.opRevolve","SWEPT_BODY",BODY,{"disambiguationData":[OSD([sQuery(id+"F0.wireOp",EDGE,"E1")])]}),"instanceName":"1"}),"instanceName":"1"}),"instanceName":"1"}),"instanceName":"1"}),"instanceName":"1"}),"instanceName":"1"}),"instanceName":"1"}),"instanceName":"1"}),"instanceName":"1"});
            var Q2950;
            Q2950=makeQuery(id+"F13.opPattern","COPY",BODY,{"derivedFrom":makeQuery(id+"F12.opPattern","COPY",BODY,{"derivedFrom":makeQuery(id+"F11.opPattern","COPY",BODY,{"derivedFrom":makeQuery(id+"F10.opPattern","COPY",BODY,{"derivedFrom":makeQuery(id+"F8.opPattern","COPY",BODY,{"derivedFrom":makeQuery(id+"F6.opPattern","COPY",BODY,{"derivedFrom":makeQuery(id+"F5.opPattern","COPY",BODY,{"derivedFrom":makeQuery(id+"F4.opPattern","COPY",BODY,{"derivedFrom":makeQuery(id+"F3.opPattern","COPY",BODY,{"derivedFrom":makeQuery(id+"F2.opPattern","COPY",BODY,{"derivedFrom":makeQuery(id+"F1.opRevolve","SWEPT_BODY",BODY,{"disambiguationData":[OSD([sQuery(id+"F0.wireOp",EDGE,"E1")])]}),"instanceName":"1"}),"instanceName":"1"}),"instanceName":"1"}),"instanceName":"1"}),"instanceName":"1"}),"instanceName":"1"}),"instanceName":"1"}),"instanceName":"1"}),"instanceName":"1"}),"instanceName":"1"});
            var Q2951;
            Q2951=makeQuery(id+"F13.opPattern","COPY",BODY,{"derivedFrom":makeQuery(id+"F12.opPattern","COPY",BODY,{"derivedFrom":makeQuery(id+"F11.opPattern","COPY",BODY,{"derivedFrom":makeQuery(id+"F10.opPattern","COPY",BODY,{"derivedFrom":makeQuery(id+"F8.opPattern","COPY",BODY,{"derivedFrom":makeQuery(id+"F7.opPattern","COPY",BODY,{"derivedFrom":makeQuery(id+"F1.opRevolve","SWEPT_BODY",BODY,{"disambiguationData":[OSD([sQuery(id+"F0.wireOp",EDGE,"E1")])]}),"instanceName":"1"}),"instanceName":"1"}),"instanceName":"1"}),"instanceName":"1"}),"instanceName":"1"}),"instanceName":"1"});
            var Q2952;
            Q2952=makeQuery(id+"F13.opPattern","COPY",BODY,{"derivedFrom":makeQuery(id+"F12.opPattern","COPY",BODY,{"derivedFrom":makeQuery(id+"F11.opPattern","COPY",BODY,{"derivedFrom":makeQuery(id+"F10.opPattern","COPY",BODY,{"derivedFrom":makeQuery(id+"F8.opPattern","COPY",BODY,{"derivedFrom":makeQuery(id+"F7.opPattern","COPY",BODY,{"derivedFrom":makeQuery(id+"F2.opPattern","COPY",BODY,{"derivedFrom":makeQuery(id+"F1.opRevolve","SWEPT_BODY",BODY,{"disambiguationData":[OSD([sQuery(id+"F0.wireOp",EDGE,"E1")])]}),"instanceName":"1"}),"instanceName":"1"}),"instanceName":"1"}),"instanceName":"1"}),"instanceName":"1"}),"instanceName":"1"}),"instanceName":"1"});
            var Q2953;
            Q2953=makeQuery(id+"F13.opPattern","COPY",BODY,{"derivedFrom":makeQuery(id+"F12.opPattern","COPY",BODY,{"derivedFrom":makeQuery(id+"F11.opPattern","COPY",BODY,{"derivedFrom":makeQuery(id+"F10.opPattern","COPY",BODY,{"derivedFrom":makeQuery(id+"F8.opPattern","COPY",BODY,{"derivedFrom":makeQuery(id+"F7.opPattern","COPY",BODY,{"derivedFrom":makeQuery(id+"F3.opPattern","COPY",BODY,{"derivedFrom":makeQuery(id+"F2.opPattern","COPY",BODY,{"derivedFrom":makeQuery(id+"F1.opRevolve","SWEPT_BODY",BODY,{"disambiguationData":[OSD([sQuery(id+"F0.wireOp",EDGE,"E1")])]}),"instanceName":"1"}),"instanceName":"1"}),"instanceName":"1"}),"instanceName":"1"}),"instanceName":"1"}),"instanceName":"1"}),"instanceName":"1"}),"instanceName":"1"});
            var Q2954;
            Q2954=makeQuery(id+"F13.opPattern","COPY",BODY,{"derivedFrom":makeQuery(id+"F12.opPattern","COPY",BODY,{"derivedFrom":makeQuery(id+"F11.opPattern","COPY",BODY,{"derivedFrom":makeQuery(id+"F10.opPattern","COPY",BODY,{"derivedFrom":makeQuery(id+"F8.opPattern","COPY",BODY,{"derivedFrom":makeQuery(id+"F7.opPattern","COPY",BODY,{"derivedFrom":makeQuery(id+"F4.opPattern","COPY",BODY,{"derivedFrom":makeQuery(id+"F1.opRevolve","SWEPT_BODY",BODY,{"disambiguationData":[OSD([sQuery(id+"F0.wireOp",EDGE,"E1")])]}),"instanceName":"1"}),"instanceName":"1"}),"instanceName":"1"}),"instanceName":"1"}),"instanceName":"1"}),"instanceName":"1"}),"instanceName":"1"});
            var Q2955;
            Q2955=makeQuery(id+"F13.opPattern","COPY",BODY,{"derivedFrom":makeQuery(id+"F12.opPattern","COPY",BODY,{"derivedFrom":makeQuery(id+"F11.opPattern","COPY",BODY,{"derivedFrom":makeQuery(id+"F10.opPattern","COPY",BODY,{"derivedFrom":makeQuery(id+"F8.opPattern","COPY",BODY,{"derivedFrom":makeQuery(id+"F7.opPattern","COPY",BODY,{"derivedFrom":makeQuery(id+"F4.opPattern","COPY",BODY,{"derivedFrom":makeQuery(id+"F2.opPattern","COPY",BODY,{"derivedFrom":makeQuery(id+"F1.opRevolve","SWEPT_BODY",BODY,{"disambiguationData":[OSD([sQuery(id+"F0.wireOp",EDGE,"E1")])]}),"instanceName":"1"}),"instanceName":"1"}),"instanceName":"1"}),"instanceName":"1"}),"instanceName":"1"}),"instanceName":"1"}),"instanceName":"1"}),"instanceName":"1"});
            var Q2956;
            Q2956=makeQuery(id+"F13.opPattern","COPY",BODY,{"derivedFrom":makeQuery(id+"F12.opPattern","COPY",BODY,{"derivedFrom":makeQuery(id+"F11.opPattern","COPY",BODY,{"derivedFrom":makeQuery(id+"F10.opPattern","COPY",BODY,{"derivedFrom":makeQuery(id+"F8.opPattern","COPY",BODY,{"derivedFrom":makeQuery(id+"F7.opPattern","COPY",BODY,{"derivedFrom":makeQuery(id+"F4.opPattern","COPY",BODY,{"derivedFrom":makeQuery(id+"F3.opPattern","COPY",BODY,{"derivedFrom":makeQuery(id+"F2.opPattern","COPY",BODY,{"derivedFrom":makeQuery(id+"F1.opRevolve","SWEPT_BODY",BODY,{"disambiguationData":[OSD([sQuery(id+"F0.wireOp",EDGE,"E1")])]}),"instanceName":"1"}),"instanceName":"1"}),"instanceName":"1"}),"instanceName":"1"}),"instanceName":"1"}),"instanceName":"1"}),"instanceName":"1"}),"instanceName":"1"}),"instanceName":"1"});
            var Q2957;
            Q2957=makeQuery(id+"F13.opPattern","COPY",BODY,{"derivedFrom":makeQuery(id+"F12.opPattern","COPY",BODY,{"derivedFrom":makeQuery(id+"F11.opPattern","COPY",BODY,{"derivedFrom":makeQuery(id+"F10.opPattern","COPY",BODY,{"derivedFrom":makeQuery(id+"F8.opPattern","COPY",BODY,{"derivedFrom":makeQuery(id+"F7.opPattern","COPY",BODY,{"derivedFrom":makeQuery(id+"F5.opPattern","COPY",BODY,{"derivedFrom":makeQuery(id+"F1.opRevolve","SWEPT_BODY",BODY,{"disambiguationData":[OSD([sQuery(id+"F0.wireOp",EDGE,"E1")])]}),"instanceName":"1"}),"instanceName":"1"}),"instanceName":"1"}),"instanceName":"1"}),"instanceName":"1"}),"instanceName":"1"}),"instanceName":"1"});
            var Q2958;
            Q2958=makeQuery(id+"F13.opPattern","COPY",BODY,{"derivedFrom":makeQuery(id+"F12.opPattern","COPY",BODY,{"derivedFrom":makeQuery(id+"F11.opPattern","COPY",BODY,{"derivedFrom":makeQuery(id+"F10.opPattern","COPY",BODY,{"derivedFrom":makeQuery(id+"F8.opPattern","COPY",BODY,{"derivedFrom":makeQuery(id+"F7.opPattern","COPY",BODY,{"derivedFrom":makeQuery(id+"F5.opPattern","COPY",BODY,{"derivedFrom":makeQuery(id+"F2.opPattern","COPY",BODY,{"derivedFrom":makeQuery(id+"F1.opRevolve","SWEPT_BODY",BODY,{"disambiguationData":[OSD([sQuery(id+"F0.wireOp",EDGE,"E1")])]}),"instanceName":"1"}),"instanceName":"1"}),"instanceName":"1"}),"instanceName":"1"}),"instanceName":"1"}),"instanceName":"1"}),"instanceName":"1"}),"instanceName":"1"});
            var Q2959;
            Q2959=makeQuery(id+"F13.opPattern","COPY",BODY,{"derivedFrom":makeQuery(id+"F12.opPattern","COPY",BODY,{"derivedFrom":makeQuery(id+"F11.opPattern","COPY",BODY,{"derivedFrom":makeQuery(id+"F10.opPattern","COPY",BODY,{"derivedFrom":makeQuery(id+"F8.opPattern","COPY",BODY,{"derivedFrom":makeQuery(id+"F7.opPattern","COPY",BODY,{"derivedFrom":makeQuery(id+"F5.opPattern","COPY",BODY,{"derivedFrom":makeQuery(id+"F3.opPattern","COPY",BODY,{"derivedFrom":makeQuery(id+"F2.opPattern","COPY",BODY,{"derivedFrom":makeQuery(id+"F1.opRevolve","SWEPT_BODY",BODY,{"disambiguationData":[OSD([sQuery(id+"F0.wireOp",EDGE,"E1")])]}),"instanceName":"1"}),"instanceName":"1"}),"instanceName":"1"}),"instanceName":"1"}),"instanceName":"1"}),"instanceName":"1"}),"instanceName":"1"}),"instanceName":"1"}),"instanceName":"1"});
            var Q2960;
            Q2960=makeQuery(id+"F13.opPattern","COPY",BODY,{"derivedFrom":makeQuery(id+"F12.opPattern","COPY",BODY,{"derivedFrom":makeQuery(id+"F11.opPattern","COPY",BODY,{"derivedFrom":makeQuery(id+"F10.opPattern","COPY",BODY,{"derivedFrom":makeQuery(id+"F8.opPattern","COPY",BODY,{"derivedFrom":makeQuery(id+"F7.opPattern","COPY",BODY,{"derivedFrom":makeQuery(id+"F5.opPattern","COPY",BODY,{"derivedFrom":makeQuery(id+"F4.opPattern","COPY",BODY,{"derivedFrom":makeQuery(id+"F1.opRevolve","SWEPT_BODY",BODY,{"disambiguationData":[OSD([sQuery(id+"F0.wireOp",EDGE,"E1")])]}),"instanceName":"1"}),"instanceName":"1"}),"instanceName":"1"}),"instanceName":"1"}),"instanceName":"1"}),"instanceName":"1"}),"instanceName":"1"}),"instanceName":"1"});
            var Q2961;
            Q2961=makeQuery(id+"F13.opPattern","COPY",BODY,{"derivedFrom":makeQuery(id+"F12.opPattern","COPY",BODY,{"derivedFrom":makeQuery(id+"F11.opPattern","COPY",BODY,{"derivedFrom":makeQuery(id+"F10.opPattern","COPY",BODY,{"derivedFrom":makeQuery(id+"F8.opPattern","COPY",BODY,{"derivedFrom":makeQuery(id+"F7.opPattern","COPY",BODY,{"derivedFrom":makeQuery(id+"F5.opPattern","COPY",BODY,{"derivedFrom":makeQuery(id+"F4.opPattern","COPY",BODY,{"derivedFrom":makeQuery(id+"F2.opPattern","COPY",BODY,{"derivedFrom":makeQuery(id+"F1.opRevolve","SWEPT_BODY",BODY,{"disambiguationData":[OSD([sQuery(id+"F0.wireOp",EDGE,"E1")])]}),"instanceName":"1"}),"instanceName":"1"}),"instanceName":"1"}),"instanceName":"1"}),"instanceName":"1"}),"instanceName":"1"}),"instanceName":"1"}),"instanceName":"1"}),"instanceName":"1"});
            var Q2962;
            Q2962=makeQuery(id+"F13.opPattern","COPY",BODY,{"derivedFrom":makeQuery(id+"F12.opPattern","COPY",BODY,{"derivedFrom":makeQuery(id+"F11.opPattern","COPY",BODY,{"derivedFrom":makeQuery(id+"F10.opPattern","COPY",BODY,{"derivedFrom":makeQuery(id+"F8.opPattern","COPY",BODY,{"derivedFrom":makeQuery(id+"F7.opPattern","COPY",BODY,{"derivedFrom":makeQuery(id+"F5.opPattern","COPY",BODY,{"derivedFrom":makeQuery(id+"F4.opPattern","COPY",BODY,{"derivedFrom":makeQuery(id+"F3.opPattern","COPY",BODY,{"derivedFrom":makeQuery(id+"F2.opPattern","COPY",BODY,{"derivedFrom":makeQuery(id+"F1.opRevolve","SWEPT_BODY",BODY,{"disambiguationData":[OSD([sQuery(id+"F0.wireOp",EDGE,"E1")])]}),"instanceName":"1"}),"instanceName":"1"}),"instanceName":"1"}),"instanceName":"1"}),"instanceName":"1"}),"instanceName":"1"}),"instanceName":"1"}),"instanceName":"1"}),"instanceName":"1"}),"instanceName":"1"});
            var Q2963;
            Q2963=makeQuery(id+"F13.opPattern","COPY",BODY,{"derivedFrom":makeQuery(id+"F12.opPattern","COPY",BODY,{"derivedFrom":makeQuery(id+"F11.opPattern","COPY",BODY,{"derivedFrom":makeQuery(id+"F10.opPattern","COPY",BODY,{"derivedFrom":makeQuery(id+"F8.opPattern","COPY",BODY,{"derivedFrom":makeQuery(id+"F7.opPattern","COPY",BODY,{"derivedFrom":makeQuery(id+"F6.opPattern","COPY",BODY,{"derivedFrom":makeQuery(id+"F1.opRevolve","SWEPT_BODY",BODY,{"disambiguationData":[OSD([sQuery(id+"F0.wireOp",EDGE,"E1")])]}),"instanceName":"1"}),"instanceName":"1"}),"instanceName":"1"}),"instanceName":"1"}),"instanceName":"1"}),"instanceName":"1"}),"instanceName":"1"});
            var Q2964;
            Q2964=makeQuery(id+"F13.opPattern","COPY",BODY,{"derivedFrom":makeQuery(id+"F12.opPattern","COPY",BODY,{"derivedFrom":makeQuery(id+"F11.opPattern","COPY",BODY,{"derivedFrom":makeQuery(id+"F10.opPattern","COPY",BODY,{"derivedFrom":makeQuery(id+"F8.opPattern","COPY",BODY,{"derivedFrom":makeQuery(id+"F7.opPattern","COPY",BODY,{"derivedFrom":makeQuery(id+"F6.opPattern","COPY",BODY,{"derivedFrom":makeQuery(id+"F2.opPattern","COPY",BODY,{"derivedFrom":makeQuery(id+"F1.opRevolve","SWEPT_BODY",BODY,{"disambiguationData":[OSD([sQuery(id+"F0.wireOp",EDGE,"E1")])]}),"instanceName":"1"}),"instanceName":"1"}),"instanceName":"1"}),"instanceName":"1"}),"instanceName":"1"}),"instanceName":"1"}),"instanceName":"1"}),"instanceName":"1"});
            var Q2965;
            Q2965=makeQuery(id+"F13.opPattern","COPY",BODY,{"derivedFrom":makeQuery(id+"F12.opPattern","COPY",BODY,{"derivedFrom":makeQuery(id+"F11.opPattern","COPY",BODY,{"derivedFrom":makeQuery(id+"F10.opPattern","COPY",BODY,{"derivedFrom":makeQuery(id+"F8.opPattern","COPY",BODY,{"derivedFrom":makeQuery(id+"F7.opPattern","COPY",BODY,{"derivedFrom":makeQuery(id+"F6.opPattern","COPY",BODY,{"derivedFrom":makeQuery(id+"F3.opPattern","COPY",BODY,{"derivedFrom":makeQuery(id+"F2.opPattern","COPY",BODY,{"derivedFrom":makeQuery(id+"F1.opRevolve","SWEPT_BODY",BODY,{"disambiguationData":[OSD([sQuery(id+"F0.wireOp",EDGE,"E1")])]}),"instanceName":"1"}),"instanceName":"1"}),"instanceName":"1"}),"instanceName":"1"}),"instanceName":"1"}),"instanceName":"1"}),"instanceName":"1"}),"instanceName":"1"}),"instanceName":"1"});
            var Q2966;
            Q2966=makeQuery(id+"F13.opPattern","COPY",BODY,{"derivedFrom":makeQuery(id+"F12.opPattern","COPY",BODY,{"derivedFrom":makeQuery(id+"F11.opPattern","COPY",BODY,{"derivedFrom":makeQuery(id+"F10.opPattern","COPY",BODY,{"derivedFrom":makeQuery(id+"F8.opPattern","COPY",BODY,{"derivedFrom":makeQuery(id+"F7.opPattern","COPY",BODY,{"derivedFrom":makeQuery(id+"F6.opPattern","COPY",BODY,{"derivedFrom":makeQuery(id+"F4.opPattern","COPY",BODY,{"derivedFrom":makeQuery(id+"F1.opRevolve","SWEPT_BODY",BODY,{"disambiguationData":[OSD([sQuery(id+"F0.wireOp",EDGE,"E1")])]}),"instanceName":"1"}),"instanceName":"1"}),"instanceName":"1"}),"instanceName":"1"}),"instanceName":"1"}),"instanceName":"1"}),"instanceName":"1"}),"instanceName":"1"});
            var Q2967;
            Q2967=makeQuery(id+"F13.opPattern","COPY",BODY,{"derivedFrom":makeQuery(id+"F12.opPattern","COPY",BODY,{"derivedFrom":makeQuery(id+"F11.opPattern","COPY",BODY,{"derivedFrom":makeQuery(id+"F10.opPattern","COPY",BODY,{"derivedFrom":makeQuery(id+"F8.opPattern","COPY",BODY,{"derivedFrom":makeQuery(id+"F7.opPattern","COPY",BODY,{"derivedFrom":makeQuery(id+"F6.opPattern","COPY",BODY,{"derivedFrom":makeQuery(id+"F4.opPattern","COPY",BODY,{"derivedFrom":makeQuery(id+"F2.opPattern","COPY",BODY,{"derivedFrom":makeQuery(id+"F1.opRevolve","SWEPT_BODY",BODY,{"disambiguationData":[OSD([sQuery(id+"F0.wireOp",EDGE,"E1")])]}),"instanceName":"1"}),"instanceName":"1"}),"instanceName":"1"}),"instanceName":"1"}),"instanceName":"1"}),"instanceName":"1"}),"instanceName":"1"}),"instanceName":"1"}),"instanceName":"1"});
            var Q2968;
            Q2968=makeQuery(id+"F13.opPattern","COPY",BODY,{"derivedFrom":makeQuery(id+"F12.opPattern","COPY",BODY,{"derivedFrom":makeQuery(id+"F11.opPattern","COPY",BODY,{"derivedFrom":makeQuery(id+"F10.opPattern","COPY",BODY,{"derivedFrom":makeQuery(id+"F8.opPattern","COPY",BODY,{"derivedFrom":makeQuery(id+"F7.opPattern","COPY",BODY,{"derivedFrom":makeQuery(id+"F6.opPattern","COPY",BODY,{"derivedFrom":makeQuery(id+"F4.opPattern","COPY",BODY,{"derivedFrom":makeQuery(id+"F3.opPattern","COPY",BODY,{"derivedFrom":makeQuery(id+"F2.opPattern","COPY",BODY,{"derivedFrom":makeQuery(id+"F1.opRevolve","SWEPT_BODY",BODY,{"disambiguationData":[OSD([sQuery(id+"F0.wireOp",EDGE,"E1")])]}),"instanceName":"1"}),"instanceName":"1"}),"instanceName":"1"}),"instanceName":"1"}),"instanceName":"1"}),"instanceName":"1"}),"instanceName":"1"}),"instanceName":"1"}),"instanceName":"1"}),"instanceName":"1"});
            var Q2969;
            Q2969=makeQuery(id+"F13.opPattern","COPY",BODY,{"derivedFrom":makeQuery(id+"F12.opPattern","COPY",BODY,{"derivedFrom":makeQuery(id+"F11.opPattern","COPY",BODY,{"derivedFrom":makeQuery(id+"F10.opPattern","COPY",BODY,{"derivedFrom":makeQuery(id+"F8.opPattern","COPY",BODY,{"derivedFrom":makeQuery(id+"F7.opPattern","COPY",BODY,{"derivedFrom":makeQuery(id+"F6.opPattern","COPY",BODY,{"derivedFrom":makeQuery(id+"F5.opPattern","COPY",BODY,{"derivedFrom":makeQuery(id+"F1.opRevolve","SWEPT_BODY",BODY,{"disambiguationData":[OSD([sQuery(id+"F0.wireOp",EDGE,"E1")])]}),"instanceName":"1"}),"instanceName":"1"}),"instanceName":"1"}),"instanceName":"1"}),"instanceName":"1"}),"instanceName":"1"}),"instanceName":"1"}),"instanceName":"1"});
            var Q2970;
            Q2970=makeQuery(id+"F13.opPattern","COPY",BODY,{"derivedFrom":makeQuery(id+"F12.opPattern","COPY",BODY,{"derivedFrom":makeQuery(id+"F11.opPattern","COPY",BODY,{"derivedFrom":makeQuery(id+"F10.opPattern","COPY",BODY,{"derivedFrom":makeQuery(id+"F8.opPattern","COPY",BODY,{"derivedFrom":makeQuery(id+"F7.opPattern","COPY",BODY,{"derivedFrom":makeQuery(id+"F6.opPattern","COPY",BODY,{"derivedFrom":makeQuery(id+"F5.opPattern","COPY",BODY,{"derivedFrom":makeQuery(id+"F2.opPattern","COPY",BODY,{"derivedFrom":makeQuery(id+"F1.opRevolve","SWEPT_BODY",BODY,{"disambiguationData":[OSD([sQuery(id+"F0.wireOp",EDGE,"E1")])]}),"instanceName":"1"}),"instanceName":"1"}),"instanceName":"1"}),"instanceName":"1"}),"instanceName":"1"}),"instanceName":"1"}),"instanceName":"1"}),"instanceName":"1"}),"instanceName":"1"});
            var Q2971;
            Q2971=makeQuery(id+"F13.opPattern","COPY",BODY,{"derivedFrom":makeQuery(id+"F12.opPattern","COPY",BODY,{"derivedFrom":makeQuery(id+"F11.opPattern","COPY",BODY,{"derivedFrom":makeQuery(id+"F10.opPattern","COPY",BODY,{"derivedFrom":makeQuery(id+"F8.opPattern","COPY",BODY,{"derivedFrom":makeQuery(id+"F7.opPattern","COPY",BODY,{"derivedFrom":makeQuery(id+"F6.opPattern","COPY",BODY,{"derivedFrom":makeQuery(id+"F5.opPattern","COPY",BODY,{"derivedFrom":makeQuery(id+"F3.opPattern","COPY",BODY,{"derivedFrom":makeQuery(id+"F2.opPattern","COPY",BODY,{"derivedFrom":makeQuery(id+"F1.opRevolve","SWEPT_BODY",BODY,{"disambiguationData":[OSD([sQuery(id+"F0.wireOp",EDGE,"E1")])]}),"instanceName":"1"}),"instanceName":"1"}),"instanceName":"1"}),"instanceName":"1"}),"instanceName":"1"}),"instanceName":"1"}),"instanceName":"1"}),"instanceName":"1"}),"instanceName":"1"}),"instanceName":"1"});
            var Q2972;
            Q2972=makeQuery(id+"F13.opPattern","COPY",BODY,{"derivedFrom":makeQuery(id+"F12.opPattern","COPY",BODY,{"derivedFrom":makeQuery(id+"F11.opPattern","COPY",BODY,{"derivedFrom":makeQuery(id+"F10.opPattern","COPY",BODY,{"derivedFrom":makeQuery(id+"F8.opPattern","COPY",BODY,{"derivedFrom":makeQuery(id+"F7.opPattern","COPY",BODY,{"derivedFrom":makeQuery(id+"F6.opPattern","COPY",BODY,{"derivedFrom":makeQuery(id+"F5.opPattern","COPY",BODY,{"derivedFrom":makeQuery(id+"F4.opPattern","COPY",BODY,{"derivedFrom":makeQuery(id+"F1.opRevolve","SWEPT_BODY",BODY,{"disambiguationData":[OSD([sQuery(id+"F0.wireOp",EDGE,"E1")])]}),"instanceName":"1"}),"instanceName":"1"}),"instanceName":"1"}),"instanceName":"1"}),"instanceName":"1"}),"instanceName":"1"}),"instanceName":"1"}),"instanceName":"1"}),"instanceName":"1"});
            var Q2973;
            Q2973=makeQuery(id+"F13.opPattern","COPY",BODY,{"derivedFrom":makeQuery(id+"F12.opPattern","COPY",BODY,{"derivedFrom":makeQuery(id+"F11.opPattern","COPY",BODY,{"derivedFrom":makeQuery(id+"F10.opPattern","COPY",BODY,{"derivedFrom":makeQuery(id+"F8.opPattern","COPY",BODY,{"derivedFrom":makeQuery(id+"F7.opPattern","COPY",BODY,{"derivedFrom":makeQuery(id+"F6.opPattern","COPY",BODY,{"derivedFrom":makeQuery(id+"F5.opPattern","COPY",BODY,{"derivedFrom":makeQuery(id+"F4.opPattern","COPY",BODY,{"derivedFrom":makeQuery(id+"F2.opPattern","COPY",BODY,{"derivedFrom":makeQuery(id+"F1.opRevolve","SWEPT_BODY",BODY,{"disambiguationData":[OSD([sQuery(id+"F0.wireOp",EDGE,"E1")])]}),"instanceName":"1"}),"instanceName":"1"}),"instanceName":"1"}),"instanceName":"1"}),"instanceName":"1"}),"instanceName":"1"}),"instanceName":"1"}),"instanceName":"1"}),"instanceName":"1"}),"instanceName":"1"});
            var Q2974;
            Q2974=makeQuery(id+"F13.opPattern","COPY",BODY,{"derivedFrom":makeQuery(id+"F12.opPattern","COPY",BODY,{"derivedFrom":makeQuery(id+"F11.opPattern","COPY",BODY,{"derivedFrom":makeQuery(id+"F10.opPattern","COPY",BODY,{"derivedFrom":makeQuery(id+"F8.opPattern","COPY",BODY,{"derivedFrom":makeQuery(id+"F7.opPattern","COPY",BODY,{"derivedFrom":makeQuery(id+"F6.opPattern","COPY",BODY,{"derivedFrom":makeQuery(id+"F5.opPattern","COPY",BODY,{"derivedFrom":makeQuery(id+"F4.opPattern","COPY",BODY,{"derivedFrom":makeQuery(id+"F3.opPattern","COPY",BODY,{"derivedFrom":makeQuery(id+"F2.opPattern","COPY",BODY,{"derivedFrom":makeQuery(id+"F1.opRevolve","SWEPT_BODY",BODY,{"disambiguationData":[OSD([sQuery(id+"F0.wireOp",EDGE,"E1")])]}),"instanceName":"1"}),"instanceName":"1"}),"instanceName":"1"}),"instanceName":"1"}),"instanceName":"1"}),"instanceName":"1"}),"instanceName":"1"}),"instanceName":"1"}),"instanceName":"1"}),"instanceName":"1"}),"instanceName":"1"});
            var Q2975;
            Q2975=makeQuery(id+"F13.opPattern","COPY",BODY,{"derivedFrom":makeQuery(id+"F12.opPattern","COPY",BODY,{"derivedFrom":makeQuery(id+"F11.opPattern","COPY",BODY,{"derivedFrom":makeQuery(id+"F10.opPattern","COPY",BODY,{"derivedFrom":makeQuery(id+"F9.opPattern","COPY",BODY,{"derivedFrom":makeQuery(id+"F1.opRevolve","SWEPT_BODY",BODY,{"disambiguationData":[OSD([sQuery(id+"F0.wireOp",EDGE,"E1")])]}),"instanceName":"1"}),"instanceName":"1"}),"instanceName":"1"}),"instanceName":"1"}),"instanceName":"1"});
            var Q2976;
            Q2976=makeQuery(id+"F13.opPattern","COPY",BODY,{"derivedFrom":makeQuery(id+"F12.opPattern","COPY",BODY,{"derivedFrom":makeQuery(id+"F11.opPattern","COPY",BODY,{"derivedFrom":makeQuery(id+"F10.opPattern","COPY",BODY,{"derivedFrom":makeQuery(id+"F9.opPattern","COPY",BODY,{"derivedFrom":makeQuery(id+"F2.opPattern","COPY",BODY,{"derivedFrom":makeQuery(id+"F1.opRevolve","SWEPT_BODY",BODY,{"disambiguationData":[OSD([sQuery(id+"F0.wireOp",EDGE,"E1")])]}),"instanceName":"1"}),"instanceName":"1"}),"instanceName":"1"}),"instanceName":"1"}),"instanceName":"1"}),"instanceName":"1"});
            var Q2977;
            Q2977=makeQuery(id+"F13.opPattern","COPY",BODY,{"derivedFrom":makeQuery(id+"F12.opPattern","COPY",BODY,{"derivedFrom":makeQuery(id+"F11.opPattern","COPY",BODY,{"derivedFrom":makeQuery(id+"F10.opPattern","COPY",BODY,{"derivedFrom":makeQuery(id+"F9.opPattern","COPY",BODY,{"derivedFrom":makeQuery(id+"F3.opPattern","COPY",BODY,{"derivedFrom":makeQuery(id+"F2.opPattern","COPY",BODY,{"derivedFrom":makeQuery(id+"F1.opRevolve","SWEPT_BODY",BODY,{"disambiguationData":[OSD([sQuery(id+"F0.wireOp",EDGE,"E1")])]}),"instanceName":"1"}),"instanceName":"1"}),"instanceName":"1"}),"instanceName":"1"}),"instanceName":"1"}),"instanceName":"1"}),"instanceName":"1"});
            var Q2978;
            Q2978=makeQuery(id+"F13.opPattern","COPY",BODY,{"derivedFrom":makeQuery(id+"F12.opPattern","COPY",BODY,{"derivedFrom":makeQuery(id+"F11.opPattern","COPY",BODY,{"derivedFrom":makeQuery(id+"F10.opPattern","COPY",BODY,{"derivedFrom":makeQuery(id+"F9.opPattern","COPY",BODY,{"derivedFrom":makeQuery(id+"F4.opPattern","COPY",BODY,{"derivedFrom":makeQuery(id+"F1.opRevolve","SWEPT_BODY",BODY,{"disambiguationData":[OSD([sQuery(id+"F0.wireOp",EDGE,"E1")])]}),"instanceName":"1"}),"instanceName":"1"}),"instanceName":"1"}),"instanceName":"1"}),"instanceName":"1"}),"instanceName":"1"});
            var Q2979;
            Q2979=makeQuery(id+"F13.opPattern","COPY",BODY,{"derivedFrom":makeQuery(id+"F12.opPattern","COPY",BODY,{"derivedFrom":makeQuery(id+"F11.opPattern","COPY",BODY,{"derivedFrom":makeQuery(id+"F10.opPattern","COPY",BODY,{"derivedFrom":makeQuery(id+"F9.opPattern","COPY",BODY,{"derivedFrom":makeQuery(id+"F4.opPattern","COPY",BODY,{"derivedFrom":makeQuery(id+"F2.opPattern","COPY",BODY,{"derivedFrom":makeQuery(id+"F1.opRevolve","SWEPT_BODY",BODY,{"disambiguationData":[OSD([sQuery(id+"F0.wireOp",EDGE,"E1")])]}),"instanceName":"1"}),"instanceName":"1"}),"instanceName":"1"}),"instanceName":"1"}),"instanceName":"1"}),"instanceName":"1"}),"instanceName":"1"});
            var Q2980;
            Q2980=makeQuery(id+"F13.opPattern","COPY",BODY,{"derivedFrom":makeQuery(id+"F12.opPattern","COPY",BODY,{"derivedFrom":makeQuery(id+"F11.opPattern","COPY",BODY,{"derivedFrom":makeQuery(id+"F10.opPattern","COPY",BODY,{"derivedFrom":makeQuery(id+"F9.opPattern","COPY",BODY,{"derivedFrom":makeQuery(id+"F4.opPattern","COPY",BODY,{"derivedFrom":makeQuery(id+"F3.opPattern","COPY",BODY,{"derivedFrom":makeQuery(id+"F2.opPattern","COPY",BODY,{"derivedFrom":makeQuery(id+"F1.opRevolve","SWEPT_BODY",BODY,{"disambiguationData":[OSD([sQuery(id+"F0.wireOp",EDGE,"E1")])]}),"instanceName":"1"}),"instanceName":"1"}),"instanceName":"1"}),"instanceName":"1"}),"instanceName":"1"}),"instanceName":"1"}),"instanceName":"1"}),"instanceName":"1"});
            var Q2981;
            Q2981=makeQuery(id+"F13.opPattern","COPY",BODY,{"derivedFrom":makeQuery(id+"F12.opPattern","COPY",BODY,{"derivedFrom":makeQuery(id+"F11.opPattern","COPY",BODY,{"derivedFrom":makeQuery(id+"F10.opPattern","COPY",BODY,{"derivedFrom":makeQuery(id+"F9.opPattern","COPY",BODY,{"derivedFrom":makeQuery(id+"F5.opPattern","COPY",BODY,{"derivedFrom":makeQuery(id+"F1.opRevolve","SWEPT_BODY",BODY,{"disambiguationData":[OSD([sQuery(id+"F0.wireOp",EDGE,"E1")])]}),"instanceName":"1"}),"instanceName":"1"}),"instanceName":"1"}),"instanceName":"1"}),"instanceName":"1"}),"instanceName":"1"});
            var Q2982;
            Q2982=makeQuery(id+"F13.opPattern","COPY",BODY,{"derivedFrom":makeQuery(id+"F12.opPattern","COPY",BODY,{"derivedFrom":makeQuery(id+"F11.opPattern","COPY",BODY,{"derivedFrom":makeQuery(id+"F10.opPattern","COPY",BODY,{"derivedFrom":makeQuery(id+"F9.opPattern","COPY",BODY,{"derivedFrom":makeQuery(id+"F5.opPattern","COPY",BODY,{"derivedFrom":makeQuery(id+"F2.opPattern","COPY",BODY,{"derivedFrom":makeQuery(id+"F1.opRevolve","SWEPT_BODY",BODY,{"disambiguationData":[OSD([sQuery(id+"F0.wireOp",EDGE,"E1")])]}),"instanceName":"1"}),"instanceName":"1"}),"instanceName":"1"}),"instanceName":"1"}),"instanceName":"1"}),"instanceName":"1"}),"instanceName":"1"});
            var Q2983;
            Q2983=makeQuery(id+"F13.opPattern","COPY",BODY,{"derivedFrom":makeQuery(id+"F12.opPattern","COPY",BODY,{"derivedFrom":makeQuery(id+"F11.opPattern","COPY",BODY,{"derivedFrom":makeQuery(id+"F10.opPattern","COPY",BODY,{"derivedFrom":makeQuery(id+"F9.opPattern","COPY",BODY,{"derivedFrom":makeQuery(id+"F5.opPattern","COPY",BODY,{"derivedFrom":makeQuery(id+"F3.opPattern","COPY",BODY,{"derivedFrom":makeQuery(id+"F2.opPattern","COPY",BODY,{"derivedFrom":makeQuery(id+"F1.opRevolve","SWEPT_BODY",BODY,{"disambiguationData":[OSD([sQuery(id+"F0.wireOp",EDGE,"E1")])]}),"instanceName":"1"}),"instanceName":"1"}),"instanceName":"1"}),"instanceName":"1"}),"instanceName":"1"}),"instanceName":"1"}),"instanceName":"1"}),"instanceName":"1"});
            var Q2984;
            Q2984=makeQuery(id+"F13.opPattern","COPY",BODY,{"derivedFrom":makeQuery(id+"F12.opPattern","COPY",BODY,{"derivedFrom":makeQuery(id+"F11.opPattern","COPY",BODY,{"derivedFrom":makeQuery(id+"F10.opPattern","COPY",BODY,{"derivedFrom":makeQuery(id+"F9.opPattern","COPY",BODY,{"derivedFrom":makeQuery(id+"F5.opPattern","COPY",BODY,{"derivedFrom":makeQuery(id+"F4.opPattern","COPY",BODY,{"derivedFrom":makeQuery(id+"F1.opRevolve","SWEPT_BODY",BODY,{"disambiguationData":[OSD([sQuery(id+"F0.wireOp",EDGE,"E1")])]}),"instanceName":"1"}),"instanceName":"1"}),"instanceName":"1"}),"instanceName":"1"}),"instanceName":"1"}),"instanceName":"1"}),"instanceName":"1"});
            var Q2985;
            Q2985=makeQuery(id+"F13.opPattern","COPY",BODY,{"derivedFrom":makeQuery(id+"F12.opPattern","COPY",BODY,{"derivedFrom":makeQuery(id+"F11.opPattern","COPY",BODY,{"derivedFrom":makeQuery(id+"F10.opPattern","COPY",BODY,{"derivedFrom":makeQuery(id+"F9.opPattern","COPY",BODY,{"derivedFrom":makeQuery(id+"F5.opPattern","COPY",BODY,{"derivedFrom":makeQuery(id+"F4.opPattern","COPY",BODY,{"derivedFrom":makeQuery(id+"F2.opPattern","COPY",BODY,{"derivedFrom":makeQuery(id+"F1.opRevolve","SWEPT_BODY",BODY,{"disambiguationData":[OSD([sQuery(id+"F0.wireOp",EDGE,"E1")])]}),"instanceName":"1"}),"instanceName":"1"}),"instanceName":"1"}),"instanceName":"1"}),"instanceName":"1"}),"instanceName":"1"}),"instanceName":"1"}),"instanceName":"1"});
            var Q2986;
            Q2986=makeQuery(id+"F13.opPattern","COPY",BODY,{"derivedFrom":makeQuery(id+"F12.opPattern","COPY",BODY,{"derivedFrom":makeQuery(id+"F11.opPattern","COPY",BODY,{"derivedFrom":makeQuery(id+"F10.opPattern","COPY",BODY,{"derivedFrom":makeQuery(id+"F9.opPattern","COPY",BODY,{"derivedFrom":makeQuery(id+"F5.opPattern","COPY",BODY,{"derivedFrom":makeQuery(id+"F4.opPattern","COPY",BODY,{"derivedFrom":makeQuery(id+"F3.opPattern","COPY",BODY,{"derivedFrom":makeQuery(id+"F2.opPattern","COPY",BODY,{"derivedFrom":makeQuery(id+"F1.opRevolve","SWEPT_BODY",BODY,{"disambiguationData":[OSD([sQuery(id+"F0.wireOp",EDGE,"E1")])]}),"instanceName":"1"}),"instanceName":"1"}),"instanceName":"1"}),"instanceName":"1"}),"instanceName":"1"}),"instanceName":"1"}),"instanceName":"1"}),"instanceName":"1"}),"instanceName":"1"});
            var Q2987;
            Q2987=makeQuery(id+"F13.opPattern","COPY",BODY,{"derivedFrom":makeQuery(id+"F12.opPattern","COPY",BODY,{"derivedFrom":makeQuery(id+"F11.opPattern","COPY",BODY,{"derivedFrom":makeQuery(id+"F10.opPattern","COPY",BODY,{"derivedFrom":makeQuery(id+"F9.opPattern","COPY",BODY,{"derivedFrom":makeQuery(id+"F6.opPattern","COPY",BODY,{"derivedFrom":makeQuery(id+"F1.opRevolve","SWEPT_BODY",BODY,{"disambiguationData":[OSD([sQuery(id+"F0.wireOp",EDGE,"E1")])]}),"instanceName":"1"}),"instanceName":"1"}),"instanceName":"1"}),"instanceName":"1"}),"instanceName":"1"}),"instanceName":"1"});
            var Q2988;
            Q2988=makeQuery(id+"F13.opPattern","COPY",BODY,{"derivedFrom":makeQuery(id+"F12.opPattern","COPY",BODY,{"derivedFrom":makeQuery(id+"F11.opPattern","COPY",BODY,{"derivedFrom":makeQuery(id+"F10.opPattern","COPY",BODY,{"derivedFrom":makeQuery(id+"F9.opPattern","COPY",BODY,{"derivedFrom":makeQuery(id+"F6.opPattern","COPY",BODY,{"derivedFrom":makeQuery(id+"F2.opPattern","COPY",BODY,{"derivedFrom":makeQuery(id+"F1.opRevolve","SWEPT_BODY",BODY,{"disambiguationData":[OSD([sQuery(id+"F0.wireOp",EDGE,"E1")])]}),"instanceName":"1"}),"instanceName":"1"}),"instanceName":"1"}),"instanceName":"1"}),"instanceName":"1"}),"instanceName":"1"}),"instanceName":"1"});
            var Q2989;
            Q2989=makeQuery(id+"F13.opPattern","COPY",BODY,{"derivedFrom":makeQuery(id+"F12.opPattern","COPY",BODY,{"derivedFrom":makeQuery(id+"F11.opPattern","COPY",BODY,{"derivedFrom":makeQuery(id+"F10.opPattern","COPY",BODY,{"derivedFrom":makeQuery(id+"F9.opPattern","COPY",BODY,{"derivedFrom":makeQuery(id+"F6.opPattern","COPY",BODY,{"derivedFrom":makeQuery(id+"F3.opPattern","COPY",BODY,{"derivedFrom":makeQuery(id+"F2.opPattern","COPY",BODY,{"derivedFrom":makeQuery(id+"F1.opRevolve","SWEPT_BODY",BODY,{"disambiguationData":[OSD([sQuery(id+"F0.wireOp",EDGE,"E1")])]}),"instanceName":"1"}),"instanceName":"1"}),"instanceName":"1"}),"instanceName":"1"}),"instanceName":"1"}),"instanceName":"1"}),"instanceName":"1"}),"instanceName":"1"});
            var Q2990;
            Q2990=makeQuery(id+"F13.opPattern","COPY",BODY,{"derivedFrom":makeQuery(id+"F12.opPattern","COPY",BODY,{"derivedFrom":makeQuery(id+"F11.opPattern","COPY",BODY,{"derivedFrom":makeQuery(id+"F10.opPattern","COPY",BODY,{"derivedFrom":makeQuery(id+"F9.opPattern","COPY",BODY,{"derivedFrom":makeQuery(id+"F6.opPattern","COPY",BODY,{"derivedFrom":makeQuery(id+"F4.opPattern","COPY",BODY,{"derivedFrom":makeQuery(id+"F1.opRevolve","SWEPT_BODY",BODY,{"disambiguationData":[OSD([sQuery(id+"F0.wireOp",EDGE,"E1")])]}),"instanceName":"1"}),"instanceName":"1"}),"instanceName":"1"}),"instanceName":"1"}),"instanceName":"1"}),"instanceName":"1"}),"instanceName":"1"});
            var Q2991;
            Q2991=makeQuery(id+"F13.opPattern","COPY",BODY,{"derivedFrom":makeQuery(id+"F12.opPattern","COPY",BODY,{"derivedFrom":makeQuery(id+"F11.opPattern","COPY",BODY,{"derivedFrom":makeQuery(id+"F10.opPattern","COPY",BODY,{"derivedFrom":makeQuery(id+"F9.opPattern","COPY",BODY,{"derivedFrom":makeQuery(id+"F6.opPattern","COPY",BODY,{"derivedFrom":makeQuery(id+"F4.opPattern","COPY",BODY,{"derivedFrom":makeQuery(id+"F2.opPattern","COPY",BODY,{"derivedFrom":makeQuery(id+"F1.opRevolve","SWEPT_BODY",BODY,{"disambiguationData":[OSD([sQuery(id+"F0.wireOp",EDGE,"E1")])]}),"instanceName":"1"}),"instanceName":"1"}),"instanceName":"1"}),"instanceName":"1"}),"instanceName":"1"}),"instanceName":"1"}),"instanceName":"1"}),"instanceName":"1"});
            var Q2992;
            Q2992=makeQuery(id+"F13.opPattern","COPY",BODY,{"derivedFrom":makeQuery(id+"F12.opPattern","COPY",BODY,{"derivedFrom":makeQuery(id+"F11.opPattern","COPY",BODY,{"derivedFrom":makeQuery(id+"F10.opPattern","COPY",BODY,{"derivedFrom":makeQuery(id+"F9.opPattern","COPY",BODY,{"derivedFrom":makeQuery(id+"F6.opPattern","COPY",BODY,{"derivedFrom":makeQuery(id+"F4.opPattern","COPY",BODY,{"derivedFrom":makeQuery(id+"F3.opPattern","COPY",BODY,{"derivedFrom":makeQuery(id+"F2.opPattern","COPY",BODY,{"derivedFrom":makeQuery(id+"F1.opRevolve","SWEPT_BODY",BODY,{"disambiguationData":[OSD([sQuery(id+"F0.wireOp",EDGE,"E1")])]}),"instanceName":"1"}),"instanceName":"1"}),"instanceName":"1"}),"instanceName":"1"}),"instanceName":"1"}),"instanceName":"1"}),"instanceName":"1"}),"instanceName":"1"}),"instanceName":"1"});
            var Q2993;
            Q2993=makeQuery(id+"F13.opPattern","COPY",BODY,{"derivedFrom":makeQuery(id+"F12.opPattern","COPY",BODY,{"derivedFrom":makeQuery(id+"F11.opPattern","COPY",BODY,{"derivedFrom":makeQuery(id+"F10.opPattern","COPY",BODY,{"derivedFrom":makeQuery(id+"F9.opPattern","COPY",BODY,{"derivedFrom":makeQuery(id+"F6.opPattern","COPY",BODY,{"derivedFrom":makeQuery(id+"F5.opPattern","COPY",BODY,{"derivedFrom":makeQuery(id+"F1.opRevolve","SWEPT_BODY",BODY,{"disambiguationData":[OSD([sQuery(id+"F0.wireOp",EDGE,"E1")])]}),"instanceName":"1"}),"instanceName":"1"}),"instanceName":"1"}),"instanceName":"1"}),"instanceName":"1"}),"instanceName":"1"}),"instanceName":"1"});
            var Q2994;
            Q2994=makeQuery(id+"F13.opPattern","COPY",BODY,{"derivedFrom":makeQuery(id+"F12.opPattern","COPY",BODY,{"derivedFrom":makeQuery(id+"F11.opPattern","COPY",BODY,{"derivedFrom":makeQuery(id+"F10.opPattern","COPY",BODY,{"derivedFrom":makeQuery(id+"F9.opPattern","COPY",BODY,{"derivedFrom":makeQuery(id+"F6.opPattern","COPY",BODY,{"derivedFrom":makeQuery(id+"F5.opPattern","COPY",BODY,{"derivedFrom":makeQuery(id+"F2.opPattern","COPY",BODY,{"derivedFrom":makeQuery(id+"F1.opRevolve","SWEPT_BODY",BODY,{"disambiguationData":[OSD([sQuery(id+"F0.wireOp",EDGE,"E1")])]}),"instanceName":"1"}),"instanceName":"1"}),"instanceName":"1"}),"instanceName":"1"}),"instanceName":"1"}),"instanceName":"1"}),"instanceName":"1"}),"instanceName":"1"});
            var Q2995;
            Q2995=makeQuery(id+"F13.opPattern","COPY",BODY,{"derivedFrom":makeQuery(id+"F12.opPattern","COPY",BODY,{"derivedFrom":makeQuery(id+"F11.opPattern","COPY",BODY,{"derivedFrom":makeQuery(id+"F10.opPattern","COPY",BODY,{"derivedFrom":makeQuery(id+"F9.opPattern","COPY",BODY,{"derivedFrom":makeQuery(id+"F6.opPattern","COPY",BODY,{"derivedFrom":makeQuery(id+"F5.opPattern","COPY",BODY,{"derivedFrom":makeQuery(id+"F3.opPattern","COPY",BODY,{"derivedFrom":makeQuery(id+"F2.opPattern","COPY",BODY,{"derivedFrom":makeQuery(id+"F1.opRevolve","SWEPT_BODY",BODY,{"disambiguationData":[OSD([sQuery(id+"F0.wireOp",EDGE,"E1")])]}),"instanceName":"1"}),"instanceName":"1"}),"instanceName":"1"}),"instanceName":"1"}),"instanceName":"1"}),"instanceName":"1"}),"instanceName":"1"}),"instanceName":"1"}),"instanceName":"1"});
            var Q2996;
            Q2996=makeQuery(id+"F13.opPattern","COPY",BODY,{"derivedFrom":makeQuery(id+"F12.opPattern","COPY",BODY,{"derivedFrom":makeQuery(id+"F11.opPattern","COPY",BODY,{"derivedFrom":makeQuery(id+"F10.opPattern","COPY",BODY,{"derivedFrom":makeQuery(id+"F9.opPattern","COPY",BODY,{"derivedFrom":makeQuery(id+"F6.opPattern","COPY",BODY,{"derivedFrom":makeQuery(id+"F5.opPattern","COPY",BODY,{"derivedFrom":makeQuery(id+"F4.opPattern","COPY",BODY,{"derivedFrom":makeQuery(id+"F1.opRevolve","SWEPT_BODY",BODY,{"disambiguationData":[OSD([sQuery(id+"F0.wireOp",EDGE,"E1")])]}),"instanceName":"1"}),"instanceName":"1"}),"instanceName":"1"}),"instanceName":"1"}),"instanceName":"1"}),"instanceName":"1"}),"instanceName":"1"}),"instanceName":"1"});
            var Q2997;
            Q2997=makeQuery(id+"F13.opPattern","COPY",BODY,{"derivedFrom":makeQuery(id+"F12.opPattern","COPY",BODY,{"derivedFrom":makeQuery(id+"F11.opPattern","COPY",BODY,{"derivedFrom":makeQuery(id+"F10.opPattern","COPY",BODY,{"derivedFrom":makeQuery(id+"F9.opPattern","COPY",BODY,{"derivedFrom":makeQuery(id+"F6.opPattern","COPY",BODY,{"derivedFrom":makeQuery(id+"F5.opPattern","COPY",BODY,{"derivedFrom":makeQuery(id+"F4.opPattern","COPY",BODY,{"derivedFrom":makeQuery(id+"F2.opPattern","COPY",BODY,{"derivedFrom":makeQuery(id+"F1.opRevolve","SWEPT_BODY",BODY,{"disambiguationData":[OSD([sQuery(id+"F0.wireOp",EDGE,"E1")])]}),"instanceName":"1"}),"instanceName":"1"}),"instanceName":"1"}),"instanceName":"1"}),"instanceName":"1"}),"instanceName":"1"}),"instanceName":"1"}),"instanceName":"1"}),"instanceName":"1"});
            var Q2998;
            Q2998=makeQuery(id+"F13.opPattern","COPY",BODY,{"derivedFrom":makeQuery(id+"F12.opPattern","COPY",BODY,{"derivedFrom":makeQuery(id+"F11.opPattern","COPY",BODY,{"derivedFrom":makeQuery(id+"F10.opPattern","COPY",BODY,{"derivedFrom":makeQuery(id+"F9.opPattern","COPY",BODY,{"derivedFrom":makeQuery(id+"F6.opPattern","COPY",BODY,{"derivedFrom":makeQuery(id+"F5.opPattern","COPY",BODY,{"derivedFrom":makeQuery(id+"F4.opPattern","COPY",BODY,{"derivedFrom":makeQuery(id+"F3.opPattern","COPY",BODY,{"derivedFrom":makeQuery(id+"F2.opPattern","COPY",BODY,{"derivedFrom":makeQuery(id+"F1.opRevolve","SWEPT_BODY",BODY,{"disambiguationData":[OSD([sQuery(id+"F0.wireOp",EDGE,"E1")])]}),"instanceName":"1"}),"instanceName":"1"}),"instanceName":"1"}),"instanceName":"1"}),"instanceName":"1"}),"instanceName":"1"}),"instanceName":"1"}),"instanceName":"1"}),"instanceName":"1"}),"instanceName":"1"});
            var Q2999;
            Q2999=makeQuery(id+"F13.opPattern","COPY",BODY,{"derivedFrom":makeQuery(id+"F12.opPattern","COPY",BODY,{"derivedFrom":makeQuery(id+"F11.opPattern","COPY",BODY,{"derivedFrom":makeQuery(id+"F10.opPattern","COPY",BODY,{"derivedFrom":makeQuery(id+"F9.opPattern","COPY",BODY,{"derivedFrom":makeQuery(id+"F7.opPattern","COPY",BODY,{"derivedFrom":makeQuery(id+"F1.opRevolve","SWEPT_BODY",BODY,{"disambiguationData":[OSD([sQuery(id+"F0.wireOp",EDGE,"E1")])]}),"instanceName":"1"}),"instanceName":"1"}),"instanceName":"1"}),"instanceName":"1"}),"instanceName":"1"}),"instanceName":"1"});
            var Q3000;
            Q3000=makeQuery(id+"F13.opPattern","COPY",BODY,{"derivedFrom":makeQuery(id+"F12.opPattern","COPY",BODY,{"derivedFrom":makeQuery(id+"F11.opPattern","COPY",BODY,{"derivedFrom":makeQuery(id+"F10.opPattern","COPY",BODY,{"derivedFrom":makeQuery(id+"F9.opPattern","COPY",BODY,{"derivedFrom":makeQuery(id+"F7.opPattern","COPY",BODY,{"derivedFrom":makeQuery(id+"F2.opPattern","COPY",BODY,{"derivedFrom":makeQuery(id+"F1.opRevolve","SWEPT_BODY",BODY,{"disambiguationData":[OSD([sQuery(id+"F0.wireOp",EDGE,"E1")])]}),"instanceName":"1"}),"instanceName":"1"}),"instanceName":"1"}),"instanceName":"1"}),"instanceName":"1"}),"instanceName":"1"}),"instanceName":"1"});
            var Q3001;
            Q3001=makeQuery(id+"F13.opPattern","COPY",BODY,{"derivedFrom":makeQuery(id+"F12.opPattern","COPY",BODY,{"derivedFrom":makeQuery(id+"F11.opPattern","COPY",BODY,{"derivedFrom":makeQuery(id+"F10.opPattern","COPY",BODY,{"derivedFrom":makeQuery(id+"F9.opPattern","COPY",BODY,{"derivedFrom":makeQuery(id+"F7.opPattern","COPY",BODY,{"derivedFrom":makeQuery(id+"F3.opPattern","COPY",BODY,{"derivedFrom":makeQuery(id+"F2.opPattern","COPY",BODY,{"derivedFrom":makeQuery(id+"F1.opRevolve","SWEPT_BODY",BODY,{"disambiguationData":[OSD([sQuery(id+"F0.wireOp",EDGE,"E1")])]}),"instanceName":"1"}),"instanceName":"1"}),"instanceName":"1"}),"instanceName":"1"}),"instanceName":"1"}),"instanceName":"1"}),"instanceName":"1"}),"instanceName":"1"});
            var Q3002;
            Q3002=makeQuery(id+"F13.opPattern","COPY",BODY,{"derivedFrom":makeQuery(id+"F12.opPattern","COPY",BODY,{"derivedFrom":makeQuery(id+"F11.opPattern","COPY",BODY,{"derivedFrom":makeQuery(id+"F10.opPattern","COPY",BODY,{"derivedFrom":makeQuery(id+"F9.opPattern","COPY",BODY,{"derivedFrom":makeQuery(id+"F7.opPattern","COPY",BODY,{"derivedFrom":makeQuery(id+"F4.opPattern","COPY",BODY,{"derivedFrom":makeQuery(id+"F1.opRevolve","SWEPT_BODY",BODY,{"disambiguationData":[OSD([sQuery(id+"F0.wireOp",EDGE,"E1")])]}),"instanceName":"1"}),"instanceName":"1"}),"instanceName":"1"}),"instanceName":"1"}),"instanceName":"1"}),"instanceName":"1"}),"instanceName":"1"});
            var Q3003;
            Q3003=makeQuery(id+"F13.opPattern","COPY",BODY,{"derivedFrom":makeQuery(id+"F12.opPattern","COPY",BODY,{"derivedFrom":makeQuery(id+"F11.opPattern","COPY",BODY,{"derivedFrom":makeQuery(id+"F10.opPattern","COPY",BODY,{"derivedFrom":makeQuery(id+"F9.opPattern","COPY",BODY,{"derivedFrom":makeQuery(id+"F7.opPattern","COPY",BODY,{"derivedFrom":makeQuery(id+"F4.opPattern","COPY",BODY,{"derivedFrom":makeQuery(id+"F2.opPattern","COPY",BODY,{"derivedFrom":makeQuery(id+"F1.opRevolve","SWEPT_BODY",BODY,{"disambiguationData":[OSD([sQuery(id+"F0.wireOp",EDGE,"E1")])]}),"instanceName":"1"}),"instanceName":"1"}),"instanceName":"1"}),"instanceName":"1"}),"instanceName":"1"}),"instanceName":"1"}),"instanceName":"1"}),"instanceName":"1"});
            var Q3004;
            Q3004=makeQuery(id+"F13.opPattern","COPY",BODY,{"derivedFrom":makeQuery(id+"F12.opPattern","COPY",BODY,{"derivedFrom":makeQuery(id+"F11.opPattern","COPY",BODY,{"derivedFrom":makeQuery(id+"F10.opPattern","COPY",BODY,{"derivedFrom":makeQuery(id+"F9.opPattern","COPY",BODY,{"derivedFrom":makeQuery(id+"F7.opPattern","COPY",BODY,{"derivedFrom":makeQuery(id+"F4.opPattern","COPY",BODY,{"derivedFrom":makeQuery(id+"F3.opPattern","COPY",BODY,{"derivedFrom":makeQuery(id+"F2.opPattern","COPY",BODY,{"derivedFrom":makeQuery(id+"F1.opRevolve","SWEPT_BODY",BODY,{"disambiguationData":[OSD([sQuery(id+"F0.wireOp",EDGE,"E1")])]}),"instanceName":"1"}),"instanceName":"1"}),"instanceName":"1"}),"instanceName":"1"}),"instanceName":"1"}),"instanceName":"1"}),"instanceName":"1"}),"instanceName":"1"}),"instanceName":"1"});
            var Q3005;
            Q3005=makeQuery(id+"F13.opPattern","COPY",BODY,{"derivedFrom":makeQuery(id+"F12.opPattern","COPY",BODY,{"derivedFrom":makeQuery(id+"F11.opPattern","COPY",BODY,{"derivedFrom":makeQuery(id+"F10.opPattern","COPY",BODY,{"derivedFrom":makeQuery(id+"F9.opPattern","COPY",BODY,{"derivedFrom":makeQuery(id+"F7.opPattern","COPY",BODY,{"derivedFrom":makeQuery(id+"F5.opPattern","COPY",BODY,{"derivedFrom":makeQuery(id+"F1.opRevolve","SWEPT_BODY",BODY,{"disambiguationData":[OSD([sQuery(id+"F0.wireOp",EDGE,"E1")])]}),"instanceName":"1"}),"instanceName":"1"}),"instanceName":"1"}),"instanceName":"1"}),"instanceName":"1"}),"instanceName":"1"}),"instanceName":"1"});
            var Q3006;
            Q3006=makeQuery(id+"F13.opPattern","COPY",BODY,{"derivedFrom":makeQuery(id+"F12.opPattern","COPY",BODY,{"derivedFrom":makeQuery(id+"F11.opPattern","COPY",BODY,{"derivedFrom":makeQuery(id+"F10.opPattern","COPY",BODY,{"derivedFrom":makeQuery(id+"F9.opPattern","COPY",BODY,{"derivedFrom":makeQuery(id+"F7.opPattern","COPY",BODY,{"derivedFrom":makeQuery(id+"F5.opPattern","COPY",BODY,{"derivedFrom":makeQuery(id+"F2.opPattern","COPY",BODY,{"derivedFrom":makeQuery(id+"F1.opRevolve","SWEPT_BODY",BODY,{"disambiguationData":[OSD([sQuery(id+"F0.wireOp",EDGE,"E1")])]}),"instanceName":"1"}),"instanceName":"1"}),"instanceName":"1"}),"instanceName":"1"}),"instanceName":"1"}),"instanceName":"1"}),"instanceName":"1"}),"instanceName":"1"});
            var Q3007;
            Q3007=makeQuery(id+"F13.opPattern","COPY",BODY,{"derivedFrom":makeQuery(id+"F12.opPattern","COPY",BODY,{"derivedFrom":makeQuery(id+"F11.opPattern","COPY",BODY,{"derivedFrom":makeQuery(id+"F10.opPattern","COPY",BODY,{"derivedFrom":makeQuery(id+"F9.opPattern","COPY",BODY,{"derivedFrom":makeQuery(id+"F7.opPattern","COPY",BODY,{"derivedFrom":makeQuery(id+"F5.opPattern","COPY",BODY,{"derivedFrom":makeQuery(id+"F3.opPattern","COPY",BODY,{"derivedFrom":makeQuery(id+"F2.opPattern","COPY",BODY,{"derivedFrom":makeQuery(id+"F1.opRevolve","SWEPT_BODY",BODY,{"disambiguationData":[OSD([sQuery(id+"F0.wireOp",EDGE,"E1")])]}),"instanceName":"1"}),"instanceName":"1"}),"instanceName":"1"}),"instanceName":"1"}),"instanceName":"1"}),"instanceName":"1"}),"instanceName":"1"}),"instanceName":"1"}),"instanceName":"1"});
            var Q3008;
            Q3008=makeQuery(id+"F13.opPattern","COPY",BODY,{"derivedFrom":makeQuery(id+"F12.opPattern","COPY",BODY,{"derivedFrom":makeQuery(id+"F11.opPattern","COPY",BODY,{"derivedFrom":makeQuery(id+"F10.opPattern","COPY",BODY,{"derivedFrom":makeQuery(id+"F9.opPattern","COPY",BODY,{"derivedFrom":makeQuery(id+"F7.opPattern","COPY",BODY,{"derivedFrom":makeQuery(id+"F5.opPattern","COPY",BODY,{"derivedFrom":makeQuery(id+"F4.opPattern","COPY",BODY,{"derivedFrom":makeQuery(id+"F1.opRevolve","SWEPT_BODY",BODY,{"disambiguationData":[OSD([sQuery(id+"F0.wireOp",EDGE,"E1")])]}),"instanceName":"1"}),"instanceName":"1"}),"instanceName":"1"}),"instanceName":"1"}),"instanceName":"1"}),"instanceName":"1"}),"instanceName":"1"}),"instanceName":"1"});
            var Q3009;
            Q3009=makeQuery(id+"F13.opPattern","COPY",BODY,{"derivedFrom":makeQuery(id+"F12.opPattern","COPY",BODY,{"derivedFrom":makeQuery(id+"F11.opPattern","COPY",BODY,{"derivedFrom":makeQuery(id+"F10.opPattern","COPY",BODY,{"derivedFrom":makeQuery(id+"F9.opPattern","COPY",BODY,{"derivedFrom":makeQuery(id+"F7.opPattern","COPY",BODY,{"derivedFrom":makeQuery(id+"F5.opPattern","COPY",BODY,{"derivedFrom":makeQuery(id+"F4.opPattern","COPY",BODY,{"derivedFrom":makeQuery(id+"F2.opPattern","COPY",BODY,{"derivedFrom":makeQuery(id+"F1.opRevolve","SWEPT_BODY",BODY,{"disambiguationData":[OSD([sQuery(id+"F0.wireOp",EDGE,"E1")])]}),"instanceName":"1"}),"instanceName":"1"}),"instanceName":"1"}),"instanceName":"1"}),"instanceName":"1"}),"instanceName":"1"}),"instanceName":"1"}),"instanceName":"1"}),"instanceName":"1"});
            var Q3010;
            Q3010=makeQuery(id+"F13.opPattern","COPY",BODY,{"derivedFrom":makeQuery(id+"F12.opPattern","COPY",BODY,{"derivedFrom":makeQuery(id+"F11.opPattern","COPY",BODY,{"derivedFrom":makeQuery(id+"F10.opPattern","COPY",BODY,{"derivedFrom":makeQuery(id+"F9.opPattern","COPY",BODY,{"derivedFrom":makeQuery(id+"F7.opPattern","COPY",BODY,{"derivedFrom":makeQuery(id+"F5.opPattern","COPY",BODY,{"derivedFrom":makeQuery(id+"F4.opPattern","COPY",BODY,{"derivedFrom":makeQuery(id+"F3.opPattern","COPY",BODY,{"derivedFrom":makeQuery(id+"F2.opPattern","COPY",BODY,{"derivedFrom":makeQuery(id+"F1.opRevolve","SWEPT_BODY",BODY,{"disambiguationData":[OSD([sQuery(id+"F0.wireOp",EDGE,"E1")])]}),"instanceName":"1"}),"instanceName":"1"}),"instanceName":"1"}),"instanceName":"1"}),"instanceName":"1"}),"instanceName":"1"}),"instanceName":"1"}),"instanceName":"1"}),"instanceName":"1"}),"instanceName":"1"});
            var Q3011;
            Q3011=makeQuery(id+"F13.opPattern","COPY",BODY,{"derivedFrom":makeQuery(id+"F12.opPattern","COPY",BODY,{"derivedFrom":makeQuery(id+"F11.opPattern","COPY",BODY,{"derivedFrom":makeQuery(id+"F10.opPattern","COPY",BODY,{"derivedFrom":makeQuery(id+"F9.opPattern","COPY",BODY,{"derivedFrom":makeQuery(id+"F7.opPattern","COPY",BODY,{"derivedFrom":makeQuery(id+"F6.opPattern","COPY",BODY,{"derivedFrom":makeQuery(id+"F1.opRevolve","SWEPT_BODY",BODY,{"disambiguationData":[OSD([sQuery(id+"F0.wireOp",EDGE,"E1")])]}),"instanceName":"1"}),"instanceName":"1"}),"instanceName":"1"}),"instanceName":"1"}),"instanceName":"1"}),"instanceName":"1"}),"instanceName":"1"});
            var Q3012;
            Q3012=makeQuery(id+"F13.opPattern","COPY",BODY,{"derivedFrom":makeQuery(id+"F12.opPattern","COPY",BODY,{"derivedFrom":makeQuery(id+"F11.opPattern","COPY",BODY,{"derivedFrom":makeQuery(id+"F10.opPattern","COPY",BODY,{"derivedFrom":makeQuery(id+"F9.opPattern","COPY",BODY,{"derivedFrom":makeQuery(id+"F7.opPattern","COPY",BODY,{"derivedFrom":makeQuery(id+"F6.opPattern","COPY",BODY,{"derivedFrom":makeQuery(id+"F2.opPattern","COPY",BODY,{"derivedFrom":makeQuery(id+"F1.opRevolve","SWEPT_BODY",BODY,{"disambiguationData":[OSD([sQuery(id+"F0.wireOp",EDGE,"E1")])]}),"instanceName":"1"}),"instanceName":"1"}),"instanceName":"1"}),"instanceName":"1"}),"instanceName":"1"}),"instanceName":"1"}),"instanceName":"1"}),"instanceName":"1"});
            var Q3013;
            Q3013=makeQuery(id+"F13.opPattern","COPY",BODY,{"derivedFrom":makeQuery(id+"F12.opPattern","COPY",BODY,{"derivedFrom":makeQuery(id+"F11.opPattern","COPY",BODY,{"derivedFrom":makeQuery(id+"F10.opPattern","COPY",BODY,{"derivedFrom":makeQuery(id+"F9.opPattern","COPY",BODY,{"derivedFrom":makeQuery(id+"F7.opPattern","COPY",BODY,{"derivedFrom":makeQuery(id+"F6.opPattern","COPY",BODY,{"derivedFrom":makeQuery(id+"F3.opPattern","COPY",BODY,{"derivedFrom":makeQuery(id+"F2.opPattern","COPY",BODY,{"derivedFrom":makeQuery(id+"F1.opRevolve","SWEPT_BODY",BODY,{"disambiguationData":[OSD([sQuery(id+"F0.wireOp",EDGE,"E1")])]}),"instanceName":"1"}),"instanceName":"1"}),"instanceName":"1"}),"instanceName":"1"}),"instanceName":"1"}),"instanceName":"1"}),"instanceName":"1"}),"instanceName":"1"}),"instanceName":"1"});
            var Q3014;
            Q3014=makeQuery(id+"F13.opPattern","COPY",BODY,{"derivedFrom":makeQuery(id+"F12.opPattern","COPY",BODY,{"derivedFrom":makeQuery(id+"F11.opPattern","COPY",BODY,{"derivedFrom":makeQuery(id+"F10.opPattern","COPY",BODY,{"derivedFrom":makeQuery(id+"F9.opPattern","COPY",BODY,{"derivedFrom":makeQuery(id+"F7.opPattern","COPY",BODY,{"derivedFrom":makeQuery(id+"F6.opPattern","COPY",BODY,{"derivedFrom":makeQuery(id+"F4.opPattern","COPY",BODY,{"derivedFrom":makeQuery(id+"F1.opRevolve","SWEPT_BODY",BODY,{"disambiguationData":[OSD([sQuery(id+"F0.wireOp",EDGE,"E1")])]}),"instanceName":"1"}),"instanceName":"1"}),"instanceName":"1"}),"instanceName":"1"}),"instanceName":"1"}),"instanceName":"1"}),"instanceName":"1"}),"instanceName":"1"});
            var Q3015;
            Q3015=makeQuery(id+"F13.opPattern","COPY",BODY,{"derivedFrom":makeQuery(id+"F12.opPattern","COPY",BODY,{"derivedFrom":makeQuery(id+"F11.opPattern","COPY",BODY,{"derivedFrom":makeQuery(id+"F10.opPattern","COPY",BODY,{"derivedFrom":makeQuery(id+"F9.opPattern","COPY",BODY,{"derivedFrom":makeQuery(id+"F7.opPattern","COPY",BODY,{"derivedFrom":makeQuery(id+"F6.opPattern","COPY",BODY,{"derivedFrom":makeQuery(id+"F4.opPattern","COPY",BODY,{"derivedFrom":makeQuery(id+"F2.opPattern","COPY",BODY,{"derivedFrom":makeQuery(id+"F1.opRevolve","SWEPT_BODY",BODY,{"disambiguationData":[OSD([sQuery(id+"F0.wireOp",EDGE,"E1")])]}),"instanceName":"1"}),"instanceName":"1"}),"instanceName":"1"}),"instanceName":"1"}),"instanceName":"1"}),"instanceName":"1"}),"instanceName":"1"}),"instanceName":"1"}),"instanceName":"1"});
            var Q3016;
            Q3016=makeQuery(id+"F13.opPattern","COPY",BODY,{"derivedFrom":makeQuery(id+"F12.opPattern","COPY",BODY,{"derivedFrom":makeQuery(id+"F11.opPattern","COPY",BODY,{"derivedFrom":makeQuery(id+"F10.opPattern","COPY",BODY,{"derivedFrom":makeQuery(id+"F9.opPattern","COPY",BODY,{"derivedFrom":makeQuery(id+"F7.opPattern","COPY",BODY,{"derivedFrom":makeQuery(id+"F6.opPattern","COPY",BODY,{"derivedFrom":makeQuery(id+"F4.opPattern","COPY",BODY,{"derivedFrom":makeQuery(id+"F3.opPattern","COPY",BODY,{"derivedFrom":makeQuery(id+"F2.opPattern","COPY",BODY,{"derivedFrom":makeQuery(id+"F1.opRevolve","SWEPT_BODY",BODY,{"disambiguationData":[OSD([sQuery(id+"F0.wireOp",EDGE,"E1")])]}),"instanceName":"1"}),"instanceName":"1"}),"instanceName":"1"}),"instanceName":"1"}),"instanceName":"1"}),"instanceName":"1"}),"instanceName":"1"}),"instanceName":"1"}),"instanceName":"1"}),"instanceName":"1"});
            var Q3017;
            Q3017=makeQuery(id+"F13.opPattern","COPY",BODY,{"derivedFrom":makeQuery(id+"F12.opPattern","COPY",BODY,{"derivedFrom":makeQuery(id+"F11.opPattern","COPY",BODY,{"derivedFrom":makeQuery(id+"F10.opPattern","COPY",BODY,{"derivedFrom":makeQuery(id+"F9.opPattern","COPY",BODY,{"derivedFrom":makeQuery(id+"F7.opPattern","COPY",BODY,{"derivedFrom":makeQuery(id+"F6.opPattern","COPY",BODY,{"derivedFrom":makeQuery(id+"F5.opPattern","COPY",BODY,{"derivedFrom":makeQuery(id+"F1.opRevolve","SWEPT_BODY",BODY,{"disambiguationData":[OSD([sQuery(id+"F0.wireOp",EDGE,"E1")])]}),"instanceName":"1"}),"instanceName":"1"}),"instanceName":"1"}),"instanceName":"1"}),"instanceName":"1"}),"instanceName":"1"}),"instanceName":"1"}),"instanceName":"1"});
            var Q3018;
            Q3018=makeQuery(id+"F13.opPattern","COPY",BODY,{"derivedFrom":makeQuery(id+"F12.opPattern","COPY",BODY,{"derivedFrom":makeQuery(id+"F11.opPattern","COPY",BODY,{"derivedFrom":makeQuery(id+"F10.opPattern","COPY",BODY,{"derivedFrom":makeQuery(id+"F9.opPattern","COPY",BODY,{"derivedFrom":makeQuery(id+"F7.opPattern","COPY",BODY,{"derivedFrom":makeQuery(id+"F6.opPattern","COPY",BODY,{"derivedFrom":makeQuery(id+"F5.opPattern","COPY",BODY,{"derivedFrom":makeQuery(id+"F2.opPattern","COPY",BODY,{"derivedFrom":makeQuery(id+"F1.opRevolve","SWEPT_BODY",BODY,{"disambiguationData":[OSD([sQuery(id+"F0.wireOp",EDGE,"E1")])]}),"instanceName":"1"}),"instanceName":"1"}),"instanceName":"1"}),"instanceName":"1"}),"instanceName":"1"}),"instanceName":"1"}),"instanceName":"1"}),"instanceName":"1"}),"instanceName":"1"});
            var Q3019;
            Q3019=makeQuery(id+"F13.opPattern","COPY",BODY,{"derivedFrom":makeQuery(id+"F12.opPattern","COPY",BODY,{"derivedFrom":makeQuery(id+"F11.opPattern","COPY",BODY,{"derivedFrom":makeQuery(id+"F10.opPattern","COPY",BODY,{"derivedFrom":makeQuery(id+"F9.opPattern","COPY",BODY,{"derivedFrom":makeQuery(id+"F7.opPattern","COPY",BODY,{"derivedFrom":makeQuery(id+"F6.opPattern","COPY",BODY,{"derivedFrom":makeQuery(id+"F5.opPattern","COPY",BODY,{"derivedFrom":makeQuery(id+"F3.opPattern","COPY",BODY,{"derivedFrom":makeQuery(id+"F2.opPattern","COPY",BODY,{"derivedFrom":makeQuery(id+"F1.opRevolve","SWEPT_BODY",BODY,{"disambiguationData":[OSD([sQuery(id+"F0.wireOp",EDGE,"E1")])]}),"instanceName":"1"}),"instanceName":"1"}),"instanceName":"1"}),"instanceName":"1"}),"instanceName":"1"}),"instanceName":"1"}),"instanceName":"1"}),"instanceName":"1"}),"instanceName":"1"}),"instanceName":"1"});
            var Q3020;
            Q3020=makeQuery(id+"F13.opPattern","COPY",BODY,{"derivedFrom":makeQuery(id+"F12.opPattern","COPY",BODY,{"derivedFrom":makeQuery(id+"F11.opPattern","COPY",BODY,{"derivedFrom":makeQuery(id+"F10.opPattern","COPY",BODY,{"derivedFrom":makeQuery(id+"F9.opPattern","COPY",BODY,{"derivedFrom":makeQuery(id+"F7.opPattern","COPY",BODY,{"derivedFrom":makeQuery(id+"F6.opPattern","COPY",BODY,{"derivedFrom":makeQuery(id+"F5.opPattern","COPY",BODY,{"derivedFrom":makeQuery(id+"F4.opPattern","COPY",BODY,{"derivedFrom":makeQuery(id+"F1.opRevolve","SWEPT_BODY",BODY,{"disambiguationData":[OSD([sQuery(id+"F0.wireOp",EDGE,"E1")])]}),"instanceName":"1"}),"instanceName":"1"}),"instanceName":"1"}),"instanceName":"1"}),"instanceName":"1"}),"instanceName":"1"}),"instanceName":"1"}),"instanceName":"1"}),"instanceName":"1"});
            var Q3021;
            Q3021=makeQuery(id+"F13.opPattern","COPY",BODY,{"derivedFrom":makeQuery(id+"F12.opPattern","COPY",BODY,{"derivedFrom":makeQuery(id+"F11.opPattern","COPY",BODY,{"derivedFrom":makeQuery(id+"F10.opPattern","COPY",BODY,{"derivedFrom":makeQuery(id+"F9.opPattern","COPY",BODY,{"derivedFrom":makeQuery(id+"F7.opPattern","COPY",BODY,{"derivedFrom":makeQuery(id+"F6.opPattern","COPY",BODY,{"derivedFrom":makeQuery(id+"F5.opPattern","COPY",BODY,{"derivedFrom":makeQuery(id+"F4.opPattern","COPY",BODY,{"derivedFrom":makeQuery(id+"F2.opPattern","COPY",BODY,{"derivedFrom":makeQuery(id+"F1.opRevolve","SWEPT_BODY",BODY,{"disambiguationData":[OSD([sQuery(id+"F0.wireOp",EDGE,"E1")])]}),"instanceName":"1"}),"instanceName":"1"}),"instanceName":"1"}),"instanceName":"1"}),"instanceName":"1"}),"instanceName":"1"}),"instanceName":"1"}),"instanceName":"1"}),"instanceName":"1"}),"instanceName":"1"});
            var Q3022;
            Q3022=makeQuery(id+"F13.opPattern","COPY",BODY,{"derivedFrom":makeQuery(id+"F12.opPattern","COPY",BODY,{"derivedFrom":makeQuery(id+"F11.opPattern","COPY",BODY,{"derivedFrom":makeQuery(id+"F10.opPattern","COPY",BODY,{"derivedFrom":makeQuery(id+"F9.opPattern","COPY",BODY,{"derivedFrom":makeQuery(id+"F7.opPattern","COPY",BODY,{"derivedFrom":makeQuery(id+"F6.opPattern","COPY",BODY,{"derivedFrom":makeQuery(id+"F5.opPattern","COPY",BODY,{"derivedFrom":makeQuery(id+"F4.opPattern","COPY",BODY,{"derivedFrom":makeQuery(id+"F3.opPattern","COPY",BODY,{"derivedFrom":makeQuery(id+"F2.opPattern","COPY",BODY,{"derivedFrom":makeQuery(id+"F1.opRevolve","SWEPT_BODY",BODY,{"disambiguationData":[OSD([sQuery(id+"F0.wireOp",EDGE,"E1")])]}),"instanceName":"1"}),"instanceName":"1"}),"instanceName":"1"}),"instanceName":"1"}),"instanceName":"1"}),"instanceName":"1"}),"instanceName":"1"}),"instanceName":"1"}),"instanceName":"1"}),"instanceName":"1"}),"instanceName":"1"});
            var Q3023;
            Q3023=makeQuery(id+"F13.opPattern","COPY",BODY,{"derivedFrom":makeQuery(id+"F12.opPattern","COPY",BODY,{"derivedFrom":makeQuery(id+"F11.opPattern","COPY",BODY,{"derivedFrom":makeQuery(id+"F10.opPattern","COPY",BODY,{"derivedFrom":makeQuery(id+"F9.opPattern","COPY",BODY,{"derivedFrom":makeQuery(id+"F8.opPattern","COPY",BODY,{"derivedFrom":makeQuery(id+"F1.opRevolve","SWEPT_BODY",BODY,{"disambiguationData":[OSD([sQuery(id+"F0.wireOp",EDGE,"E1")])]}),"instanceName":"1"}),"instanceName":"1"}),"instanceName":"1"}),"instanceName":"1"}),"instanceName":"1"}),"instanceName":"1"});
            var Q3024;
            Q3024=makeQuery(id+"F13.opPattern","COPY",BODY,{"derivedFrom":makeQuery(id+"F12.opPattern","COPY",BODY,{"derivedFrom":makeQuery(id+"F11.opPattern","COPY",BODY,{"derivedFrom":makeQuery(id+"F10.opPattern","COPY",BODY,{"derivedFrom":makeQuery(id+"F9.opPattern","COPY",BODY,{"derivedFrom":makeQuery(id+"F8.opPattern","COPY",BODY,{"derivedFrom":makeQuery(id+"F2.opPattern","COPY",BODY,{"derivedFrom":makeQuery(id+"F1.opRevolve","SWEPT_BODY",BODY,{"disambiguationData":[OSD([sQuery(id+"F0.wireOp",EDGE,"E1")])]}),"instanceName":"1"}),"instanceName":"1"}),"instanceName":"1"}),"instanceName":"1"}),"instanceName":"1"}),"instanceName":"1"}),"instanceName":"1"});
            var Q3025;
            Q3025=makeQuery(id+"F13.opPattern","COPY",BODY,{"derivedFrom":makeQuery(id+"F12.opPattern","COPY",BODY,{"derivedFrom":makeQuery(id+"F11.opPattern","COPY",BODY,{"derivedFrom":makeQuery(id+"F10.opPattern","COPY",BODY,{"derivedFrom":makeQuery(id+"F9.opPattern","COPY",BODY,{"derivedFrom":makeQuery(id+"F8.opPattern","COPY",BODY,{"derivedFrom":makeQuery(id+"F3.opPattern","COPY",BODY,{"derivedFrom":makeQuery(id+"F2.opPattern","COPY",BODY,{"derivedFrom":makeQuery(id+"F1.opRevolve","SWEPT_BODY",BODY,{"disambiguationData":[OSD([sQuery(id+"F0.wireOp",EDGE,"E1")])]}),"instanceName":"1"}),"instanceName":"1"}),"instanceName":"1"}),"instanceName":"1"}),"instanceName":"1"}),"instanceName":"1"}),"instanceName":"1"}),"instanceName":"1"});
            var Q3026;
            Q3026=makeQuery(id+"F13.opPattern","COPY",BODY,{"derivedFrom":makeQuery(id+"F12.opPattern","COPY",BODY,{"derivedFrom":makeQuery(id+"F11.opPattern","COPY",BODY,{"derivedFrom":makeQuery(id+"F10.opPattern","COPY",BODY,{"derivedFrom":makeQuery(id+"F9.opPattern","COPY",BODY,{"derivedFrom":makeQuery(id+"F8.opPattern","COPY",BODY,{"derivedFrom":makeQuery(id+"F4.opPattern","COPY",BODY,{"derivedFrom":makeQuery(id+"F1.opRevolve","SWEPT_BODY",BODY,{"disambiguationData":[OSD([sQuery(id+"F0.wireOp",EDGE,"E1")])]}),"instanceName":"1"}),"instanceName":"1"}),"instanceName":"1"}),"instanceName":"1"}),"instanceName":"1"}),"instanceName":"1"}),"instanceName":"1"});
            var Q3027;
            Q3027=makeQuery(id+"F13.opPattern","COPY",BODY,{"derivedFrom":makeQuery(id+"F12.opPattern","COPY",BODY,{"derivedFrom":makeQuery(id+"F11.opPattern","COPY",BODY,{"derivedFrom":makeQuery(id+"F10.opPattern","COPY",BODY,{"derivedFrom":makeQuery(id+"F9.opPattern","COPY",BODY,{"derivedFrom":makeQuery(id+"F8.opPattern","COPY",BODY,{"derivedFrom":makeQuery(id+"F4.opPattern","COPY",BODY,{"derivedFrom":makeQuery(id+"F2.opPattern","COPY",BODY,{"derivedFrom":makeQuery(id+"F1.opRevolve","SWEPT_BODY",BODY,{"disambiguationData":[OSD([sQuery(id+"F0.wireOp",EDGE,"E1")])]}),"instanceName":"1"}),"instanceName":"1"}),"instanceName":"1"}),"instanceName":"1"}),"instanceName":"1"}),"instanceName":"1"}),"instanceName":"1"}),"instanceName":"1"});
            var Q3028;
            Q3028=makeQuery(id+"F13.opPattern","COPY",BODY,{"derivedFrom":makeQuery(id+"F12.opPattern","COPY",BODY,{"derivedFrom":makeQuery(id+"F11.opPattern","COPY",BODY,{"derivedFrom":makeQuery(id+"F10.opPattern","COPY",BODY,{"derivedFrom":makeQuery(id+"F9.opPattern","COPY",BODY,{"derivedFrom":makeQuery(id+"F8.opPattern","COPY",BODY,{"derivedFrom":makeQuery(id+"F4.opPattern","COPY",BODY,{"derivedFrom":makeQuery(id+"F3.opPattern","COPY",BODY,{"derivedFrom":makeQuery(id+"F2.opPattern","COPY",BODY,{"derivedFrom":makeQuery(id+"F1.opRevolve","SWEPT_BODY",BODY,{"disambiguationData":[OSD([sQuery(id+"F0.wireOp",EDGE,"E1")])]}),"instanceName":"1"}),"instanceName":"1"}),"instanceName":"1"}),"instanceName":"1"}),"instanceName":"1"}),"instanceName":"1"}),"instanceName":"1"}),"instanceName":"1"}),"instanceName":"1"});
            var Q3029;
            Q3029=makeQuery(id+"F13.opPattern","COPY",BODY,{"derivedFrom":makeQuery(id+"F12.opPattern","COPY",BODY,{"derivedFrom":makeQuery(id+"F11.opPattern","COPY",BODY,{"derivedFrom":makeQuery(id+"F10.opPattern","COPY",BODY,{"derivedFrom":makeQuery(id+"F9.opPattern","COPY",BODY,{"derivedFrom":makeQuery(id+"F8.opPattern","COPY",BODY,{"derivedFrom":makeQuery(id+"F5.opPattern","COPY",BODY,{"derivedFrom":makeQuery(id+"F1.opRevolve","SWEPT_BODY",BODY,{"disambiguationData":[OSD([sQuery(id+"F0.wireOp",EDGE,"E1")])]}),"instanceName":"1"}),"instanceName":"1"}),"instanceName":"1"}),"instanceName":"1"}),"instanceName":"1"}),"instanceName":"1"}),"instanceName":"1"});
            var Q3030;
            Q3030=makeQuery(id+"F13.opPattern","COPY",BODY,{"derivedFrom":makeQuery(id+"F12.opPattern","COPY",BODY,{"derivedFrom":makeQuery(id+"F11.opPattern","COPY",BODY,{"derivedFrom":makeQuery(id+"F10.opPattern","COPY",BODY,{"derivedFrom":makeQuery(id+"F9.opPattern","COPY",BODY,{"derivedFrom":makeQuery(id+"F8.opPattern","COPY",BODY,{"derivedFrom":makeQuery(id+"F5.opPattern","COPY",BODY,{"derivedFrom":makeQuery(id+"F2.opPattern","COPY",BODY,{"derivedFrom":makeQuery(id+"F1.opRevolve","SWEPT_BODY",BODY,{"disambiguationData":[OSD([sQuery(id+"F0.wireOp",EDGE,"E1")])]}),"instanceName":"1"}),"instanceName":"1"}),"instanceName":"1"}),"instanceName":"1"}),"instanceName":"1"}),"instanceName":"1"}),"instanceName":"1"}),"instanceName":"1"});
            var Q3031;
            Q3031=makeQuery(id+"F13.opPattern","COPY",BODY,{"derivedFrom":makeQuery(id+"F12.opPattern","COPY",BODY,{"derivedFrom":makeQuery(id+"F11.opPattern","COPY",BODY,{"derivedFrom":makeQuery(id+"F10.opPattern","COPY",BODY,{"derivedFrom":makeQuery(id+"F9.opPattern","COPY",BODY,{"derivedFrom":makeQuery(id+"F8.opPattern","COPY",BODY,{"derivedFrom":makeQuery(id+"F5.opPattern","COPY",BODY,{"derivedFrom":makeQuery(id+"F3.opPattern","COPY",BODY,{"derivedFrom":makeQuery(id+"F2.opPattern","COPY",BODY,{"derivedFrom":makeQuery(id+"F1.opRevolve","SWEPT_BODY",BODY,{"disambiguationData":[OSD([sQuery(id+"F0.wireOp",EDGE,"E1")])]}),"instanceName":"1"}),"instanceName":"1"}),"instanceName":"1"}),"instanceName":"1"}),"instanceName":"1"}),"instanceName":"1"}),"instanceName":"1"}),"instanceName":"1"}),"instanceName":"1"});
            var Q3032;
            Q3032=makeQuery(id+"F13.opPattern","COPY",BODY,{"derivedFrom":makeQuery(id+"F12.opPattern","COPY",BODY,{"derivedFrom":makeQuery(id+"F11.opPattern","COPY",BODY,{"derivedFrom":makeQuery(id+"F10.opPattern","COPY",BODY,{"derivedFrom":makeQuery(id+"F9.opPattern","COPY",BODY,{"derivedFrom":makeQuery(id+"F8.opPattern","COPY",BODY,{"derivedFrom":makeQuery(id+"F5.opPattern","COPY",BODY,{"derivedFrom":makeQuery(id+"F4.opPattern","COPY",BODY,{"derivedFrom":makeQuery(id+"F1.opRevolve","SWEPT_BODY",BODY,{"disambiguationData":[OSD([sQuery(id+"F0.wireOp",EDGE,"E1")])]}),"instanceName":"1"}),"instanceName":"1"}),"instanceName":"1"}),"instanceName":"1"}),"instanceName":"1"}),"instanceName":"1"}),"instanceName":"1"}),"instanceName":"1"});
            var Q3033;
            Q3033=makeQuery(id+"F13.opPattern","COPY",BODY,{"derivedFrom":makeQuery(id+"F12.opPattern","COPY",BODY,{"derivedFrom":makeQuery(id+"F11.opPattern","COPY",BODY,{"derivedFrom":makeQuery(id+"F10.opPattern","COPY",BODY,{"derivedFrom":makeQuery(id+"F9.opPattern","COPY",BODY,{"derivedFrom":makeQuery(id+"F8.opPattern","COPY",BODY,{"derivedFrom":makeQuery(id+"F5.opPattern","COPY",BODY,{"derivedFrom":makeQuery(id+"F4.opPattern","COPY",BODY,{"derivedFrom":makeQuery(id+"F2.opPattern","COPY",BODY,{"derivedFrom":makeQuery(id+"F1.opRevolve","SWEPT_BODY",BODY,{"disambiguationData":[OSD([sQuery(id+"F0.wireOp",EDGE,"E1")])]}),"instanceName":"1"}),"instanceName":"1"}),"instanceName":"1"}),"instanceName":"1"}),"instanceName":"1"}),"instanceName":"1"}),"instanceName":"1"}),"instanceName":"1"}),"instanceName":"1"});
            var Q3034;
            Q3034=makeQuery(id+"F13.opPattern","COPY",BODY,{"derivedFrom":makeQuery(id+"F12.opPattern","COPY",BODY,{"derivedFrom":makeQuery(id+"F11.opPattern","COPY",BODY,{"derivedFrom":makeQuery(id+"F10.opPattern","COPY",BODY,{"derivedFrom":makeQuery(id+"F9.opPattern","COPY",BODY,{"derivedFrom":makeQuery(id+"F8.opPattern","COPY",BODY,{"derivedFrom":makeQuery(id+"F5.opPattern","COPY",BODY,{"derivedFrom":makeQuery(id+"F4.opPattern","COPY",BODY,{"derivedFrom":makeQuery(id+"F3.opPattern","COPY",BODY,{"derivedFrom":makeQuery(id+"F2.opPattern","COPY",BODY,{"derivedFrom":makeQuery(id+"F1.opRevolve","SWEPT_BODY",BODY,{"disambiguationData":[OSD([sQuery(id+"F0.wireOp",EDGE,"E1")])]}),"instanceName":"1"}),"instanceName":"1"}),"instanceName":"1"}),"instanceName":"1"}),"instanceName":"1"}),"instanceName":"1"}),"instanceName":"1"}),"instanceName":"1"}),"instanceName":"1"}),"instanceName":"1"});
            var Q3035;
            Q3035=makeQuery(id+"F13.opPattern","COPY",BODY,{"derivedFrom":makeQuery(id+"F12.opPattern","COPY",BODY,{"derivedFrom":makeQuery(id+"F11.opPattern","COPY",BODY,{"derivedFrom":makeQuery(id+"F10.opPattern","COPY",BODY,{"derivedFrom":makeQuery(id+"F9.opPattern","COPY",BODY,{"derivedFrom":makeQuery(id+"F8.opPattern","COPY",BODY,{"derivedFrom":makeQuery(id+"F6.opPattern","COPY",BODY,{"derivedFrom":makeQuery(id+"F1.opRevolve","SWEPT_BODY",BODY,{"disambiguationData":[OSD([sQuery(id+"F0.wireOp",EDGE,"E1")])]}),"instanceName":"1"}),"instanceName":"1"}),"instanceName":"1"}),"instanceName":"1"}),"instanceName":"1"}),"instanceName":"1"}),"instanceName":"1"});
            var Q3036;
            Q3036=makeQuery(id+"F13.opPattern","COPY",BODY,{"derivedFrom":makeQuery(id+"F12.opPattern","COPY",BODY,{"derivedFrom":makeQuery(id+"F11.opPattern","COPY",BODY,{"derivedFrom":makeQuery(id+"F10.opPattern","COPY",BODY,{"derivedFrom":makeQuery(id+"F9.opPattern","COPY",BODY,{"derivedFrom":makeQuery(id+"F8.opPattern","COPY",BODY,{"derivedFrom":makeQuery(id+"F6.opPattern","COPY",BODY,{"derivedFrom":makeQuery(id+"F2.opPattern","COPY",BODY,{"derivedFrom":makeQuery(id+"F1.opRevolve","SWEPT_BODY",BODY,{"disambiguationData":[OSD([sQuery(id+"F0.wireOp",EDGE,"E1")])]}),"instanceName":"1"}),"instanceName":"1"}),"instanceName":"1"}),"instanceName":"1"}),"instanceName":"1"}),"instanceName":"1"}),"instanceName":"1"}),"instanceName":"1"});
            var Q3037;
            Q3037=makeQuery(id+"F13.opPattern","COPY",BODY,{"derivedFrom":makeQuery(id+"F12.opPattern","COPY",BODY,{"derivedFrom":makeQuery(id+"F11.opPattern","COPY",BODY,{"derivedFrom":makeQuery(id+"F10.opPattern","COPY",BODY,{"derivedFrom":makeQuery(id+"F9.opPattern","COPY",BODY,{"derivedFrom":makeQuery(id+"F8.opPattern","COPY",BODY,{"derivedFrom":makeQuery(id+"F6.opPattern","COPY",BODY,{"derivedFrom":makeQuery(id+"F3.opPattern","COPY",BODY,{"derivedFrom":makeQuery(id+"F2.opPattern","COPY",BODY,{"derivedFrom":makeQuery(id+"F1.opRevolve","SWEPT_BODY",BODY,{"disambiguationData":[OSD([sQuery(id+"F0.wireOp",EDGE,"E1")])]}),"instanceName":"1"}),"instanceName":"1"}),"instanceName":"1"}),"instanceName":"1"}),"instanceName":"1"}),"instanceName":"1"}),"instanceName":"1"}),"instanceName":"1"}),"instanceName":"1"});
            var Q3038;
            Q3038=makeQuery(id+"F13.opPattern","COPY",BODY,{"derivedFrom":makeQuery(id+"F12.opPattern","COPY",BODY,{"derivedFrom":makeQuery(id+"F11.opPattern","COPY",BODY,{"derivedFrom":makeQuery(id+"F10.opPattern","COPY",BODY,{"derivedFrom":makeQuery(id+"F9.opPattern","COPY",BODY,{"derivedFrom":makeQuery(id+"F8.opPattern","COPY",BODY,{"derivedFrom":makeQuery(id+"F6.opPattern","COPY",BODY,{"derivedFrom":makeQuery(id+"F4.opPattern","COPY",BODY,{"derivedFrom":makeQuery(id+"F1.opRevolve","SWEPT_BODY",BODY,{"disambiguationData":[OSD([sQuery(id+"F0.wireOp",EDGE,"E1")])]}),"instanceName":"1"}),"instanceName":"1"}),"instanceName":"1"}),"instanceName":"1"}),"instanceName":"1"}),"instanceName":"1"}),"instanceName":"1"}),"instanceName":"1"});
            var Q3039;
            Q3039=makeQuery(id+"F13.opPattern","COPY",BODY,{"derivedFrom":makeQuery(id+"F12.opPattern","COPY",BODY,{"derivedFrom":makeQuery(id+"F11.opPattern","COPY",BODY,{"derivedFrom":makeQuery(id+"F10.opPattern","COPY",BODY,{"derivedFrom":makeQuery(id+"F9.opPattern","COPY",BODY,{"derivedFrom":makeQuery(id+"F8.opPattern","COPY",BODY,{"derivedFrom":makeQuery(id+"F6.opPattern","COPY",BODY,{"derivedFrom":makeQuery(id+"F4.opPattern","COPY",BODY,{"derivedFrom":makeQuery(id+"F2.opPattern","COPY",BODY,{"derivedFrom":makeQuery(id+"F1.opRevolve","SWEPT_BODY",BODY,{"disambiguationData":[OSD([sQuery(id+"F0.wireOp",EDGE,"E1")])]}),"instanceName":"1"}),"instanceName":"1"}),"instanceName":"1"}),"instanceName":"1"}),"instanceName":"1"}),"instanceName":"1"}),"instanceName":"1"}),"instanceName":"1"}),"instanceName":"1"});
            var Q3040;
            Q3040=makeQuery(id+"F13.opPattern","COPY",BODY,{"derivedFrom":makeQuery(id+"F12.opPattern","COPY",BODY,{"derivedFrom":makeQuery(id+"F11.opPattern","COPY",BODY,{"derivedFrom":makeQuery(id+"F10.opPattern","COPY",BODY,{"derivedFrom":makeQuery(id+"F9.opPattern","COPY",BODY,{"derivedFrom":makeQuery(id+"F8.opPattern","COPY",BODY,{"derivedFrom":makeQuery(id+"F6.opPattern","COPY",BODY,{"derivedFrom":makeQuery(id+"F4.opPattern","COPY",BODY,{"derivedFrom":makeQuery(id+"F3.opPattern","COPY",BODY,{"derivedFrom":makeQuery(id+"F2.opPattern","COPY",BODY,{"derivedFrom":makeQuery(id+"F1.opRevolve","SWEPT_BODY",BODY,{"disambiguationData":[OSD([sQuery(id+"F0.wireOp",EDGE,"E1")])]}),"instanceName":"1"}),"instanceName":"1"}),"instanceName":"1"}),"instanceName":"1"}),"instanceName":"1"}),"instanceName":"1"}),"instanceName":"1"}),"instanceName":"1"}),"instanceName":"1"}),"instanceName":"1"});
            var Q3041;
            Q3041=makeQuery(id+"F13.opPattern","COPY",BODY,{"derivedFrom":makeQuery(id+"F12.opPattern","COPY",BODY,{"derivedFrom":makeQuery(id+"F11.opPattern","COPY",BODY,{"derivedFrom":makeQuery(id+"F10.opPattern","COPY",BODY,{"derivedFrom":makeQuery(id+"F9.opPattern","COPY",BODY,{"derivedFrom":makeQuery(id+"F8.opPattern","COPY",BODY,{"derivedFrom":makeQuery(id+"F6.opPattern","COPY",BODY,{"derivedFrom":makeQuery(id+"F5.opPattern","COPY",BODY,{"derivedFrom":makeQuery(id+"F1.opRevolve","SWEPT_BODY",BODY,{"disambiguationData":[OSD([sQuery(id+"F0.wireOp",EDGE,"E1")])]}),"instanceName":"1"}),"instanceName":"1"}),"instanceName":"1"}),"instanceName":"1"}),"instanceName":"1"}),"instanceName":"1"}),"instanceName":"1"}),"instanceName":"1"});
            var Q3042;
            Q3042=makeQuery(id+"F13.opPattern","COPY",BODY,{"derivedFrom":makeQuery(id+"F12.opPattern","COPY",BODY,{"derivedFrom":makeQuery(id+"F11.opPattern","COPY",BODY,{"derivedFrom":makeQuery(id+"F10.opPattern","COPY",BODY,{"derivedFrom":makeQuery(id+"F9.opPattern","COPY",BODY,{"derivedFrom":makeQuery(id+"F8.opPattern","COPY",BODY,{"derivedFrom":makeQuery(id+"F6.opPattern","COPY",BODY,{"derivedFrom":makeQuery(id+"F5.opPattern","COPY",BODY,{"derivedFrom":makeQuery(id+"F2.opPattern","COPY",BODY,{"derivedFrom":makeQuery(id+"F1.opRevolve","SWEPT_BODY",BODY,{"disambiguationData":[OSD([sQuery(id+"F0.wireOp",EDGE,"E1")])]}),"instanceName":"1"}),"instanceName":"1"}),"instanceName":"1"}),"instanceName":"1"}),"instanceName":"1"}),"instanceName":"1"}),"instanceName":"1"}),"instanceName":"1"}),"instanceName":"1"});
            var Q3043;
            Q3043=makeQuery(id+"F13.opPattern","COPY",BODY,{"derivedFrom":makeQuery(id+"F12.opPattern","COPY",BODY,{"derivedFrom":makeQuery(id+"F11.opPattern","COPY",BODY,{"derivedFrom":makeQuery(id+"F10.opPattern","COPY",BODY,{"derivedFrom":makeQuery(id+"F9.opPattern","COPY",BODY,{"derivedFrom":makeQuery(id+"F8.opPattern","COPY",BODY,{"derivedFrom":makeQuery(id+"F6.opPattern","COPY",BODY,{"derivedFrom":makeQuery(id+"F5.opPattern","COPY",BODY,{"derivedFrom":makeQuery(id+"F3.opPattern","COPY",BODY,{"derivedFrom":makeQuery(id+"F2.opPattern","COPY",BODY,{"derivedFrom":makeQuery(id+"F1.opRevolve","SWEPT_BODY",BODY,{"disambiguationData":[OSD([sQuery(id+"F0.wireOp",EDGE,"E1")])]}),"instanceName":"1"}),"instanceName":"1"}),"instanceName":"1"}),"instanceName":"1"}),"instanceName":"1"}),"instanceName":"1"}),"instanceName":"1"}),"instanceName":"1"}),"instanceName":"1"}),"instanceName":"1"});
            var Q3044;
            Q3044=makeQuery(id+"F13.opPattern","COPY",BODY,{"derivedFrom":makeQuery(id+"F12.opPattern","COPY",BODY,{"derivedFrom":makeQuery(id+"F11.opPattern","COPY",BODY,{"derivedFrom":makeQuery(id+"F10.opPattern","COPY",BODY,{"derivedFrom":makeQuery(id+"F9.opPattern","COPY",BODY,{"derivedFrom":makeQuery(id+"F8.opPattern","COPY",BODY,{"derivedFrom":makeQuery(id+"F6.opPattern","COPY",BODY,{"derivedFrom":makeQuery(id+"F5.opPattern","COPY",BODY,{"derivedFrom":makeQuery(id+"F4.opPattern","COPY",BODY,{"derivedFrom":makeQuery(id+"F1.opRevolve","SWEPT_BODY",BODY,{"disambiguationData":[OSD([sQuery(id+"F0.wireOp",EDGE,"E1")])]}),"instanceName":"1"}),"instanceName":"1"}),"instanceName":"1"}),"instanceName":"1"}),"instanceName":"1"}),"instanceName":"1"}),"instanceName":"1"}),"instanceName":"1"}),"instanceName":"1"});
            var Q3045;
            Q3045=makeQuery(id+"F13.opPattern","COPY",BODY,{"derivedFrom":makeQuery(id+"F12.opPattern","COPY",BODY,{"derivedFrom":makeQuery(id+"F11.opPattern","COPY",BODY,{"derivedFrom":makeQuery(id+"F10.opPattern","COPY",BODY,{"derivedFrom":makeQuery(id+"F9.opPattern","COPY",BODY,{"derivedFrom":makeQuery(id+"F8.opPattern","COPY",BODY,{"derivedFrom":makeQuery(id+"F6.opPattern","COPY",BODY,{"derivedFrom":makeQuery(id+"F5.opPattern","COPY",BODY,{"derivedFrom":makeQuery(id+"F4.opPattern","COPY",BODY,{"derivedFrom":makeQuery(id+"F2.opPattern","COPY",BODY,{"derivedFrom":makeQuery(id+"F1.opRevolve","SWEPT_BODY",BODY,{"disambiguationData":[OSD([sQuery(id+"F0.wireOp",EDGE,"E1")])]}),"instanceName":"1"}),"instanceName":"1"}),"instanceName":"1"}),"instanceName":"1"}),"instanceName":"1"}),"instanceName":"1"}),"instanceName":"1"}),"instanceName":"1"}),"instanceName":"1"}),"instanceName":"1"});
            var Q3046;
            Q3046=makeQuery(id+"F13.opPattern","COPY",BODY,{"derivedFrom":makeQuery(id+"F12.opPattern","COPY",BODY,{"derivedFrom":makeQuery(id+"F11.opPattern","COPY",BODY,{"derivedFrom":makeQuery(id+"F10.opPattern","COPY",BODY,{"derivedFrom":makeQuery(id+"F9.opPattern","COPY",BODY,{"derivedFrom":makeQuery(id+"F8.opPattern","COPY",BODY,{"derivedFrom":makeQuery(id+"F6.opPattern","COPY",BODY,{"derivedFrom":makeQuery(id+"F5.opPattern","COPY",BODY,{"derivedFrom":makeQuery(id+"F4.opPattern","COPY",BODY,{"derivedFrom":makeQuery(id+"F3.opPattern","COPY",BODY,{"derivedFrom":makeQuery(id+"F2.opPattern","COPY",BODY,{"derivedFrom":makeQuery(id+"F1.opRevolve","SWEPT_BODY",BODY,{"disambiguationData":[OSD([sQuery(id+"F0.wireOp",EDGE,"E1")])]}),"instanceName":"1"}),"instanceName":"1"}),"instanceName":"1"}),"instanceName":"1"}),"instanceName":"1"}),"instanceName":"1"}),"instanceName":"1"}),"instanceName":"1"}),"instanceName":"1"}),"instanceName":"1"}),"instanceName":"1"});
            var Q3047;
            Q3047=makeQuery(id+"F13.opPattern","COPY",BODY,{"derivedFrom":makeQuery(id+"F12.opPattern","COPY",BODY,{"derivedFrom":makeQuery(id+"F11.opPattern","COPY",BODY,{"derivedFrom":makeQuery(id+"F10.opPattern","COPY",BODY,{"derivedFrom":makeQuery(id+"F9.opPattern","COPY",BODY,{"derivedFrom":makeQuery(id+"F8.opPattern","COPY",BODY,{"derivedFrom":makeQuery(id+"F7.opPattern","COPY",BODY,{"derivedFrom":makeQuery(id+"F1.opRevolve","SWEPT_BODY",BODY,{"disambiguationData":[OSD([sQuery(id+"F0.wireOp",EDGE,"E1")])]}),"instanceName":"1"}),"instanceName":"1"}),"instanceName":"1"}),"instanceName":"1"}),"instanceName":"1"}),"instanceName":"1"}),"instanceName":"1"});
            var Q3048;
            Q3048=makeQuery(id+"F13.opPattern","COPY",BODY,{"derivedFrom":makeQuery(id+"F12.opPattern","COPY",BODY,{"derivedFrom":makeQuery(id+"F11.opPattern","COPY",BODY,{"derivedFrom":makeQuery(id+"F10.opPattern","COPY",BODY,{"derivedFrom":makeQuery(id+"F9.opPattern","COPY",BODY,{"derivedFrom":makeQuery(id+"F8.opPattern","COPY",BODY,{"derivedFrom":makeQuery(id+"F7.opPattern","COPY",BODY,{"derivedFrom":makeQuery(id+"F2.opPattern","COPY",BODY,{"derivedFrom":makeQuery(id+"F1.opRevolve","SWEPT_BODY",BODY,{"disambiguationData":[OSD([sQuery(id+"F0.wireOp",EDGE,"E1")])]}),"instanceName":"1"}),"instanceName":"1"}),"instanceName":"1"}),"instanceName":"1"}),"instanceName":"1"}),"instanceName":"1"}),"instanceName":"1"}),"instanceName":"1"});
            var Q3049;
            Q3049=makeQuery(id+"F13.opPattern","COPY",BODY,{"derivedFrom":makeQuery(id+"F12.opPattern","COPY",BODY,{"derivedFrom":makeQuery(id+"F11.opPattern","COPY",BODY,{"derivedFrom":makeQuery(id+"F10.opPattern","COPY",BODY,{"derivedFrom":makeQuery(id+"F9.opPattern","COPY",BODY,{"derivedFrom":makeQuery(id+"F8.opPattern","COPY",BODY,{"derivedFrom":makeQuery(id+"F7.opPattern","COPY",BODY,{"derivedFrom":makeQuery(id+"F3.opPattern","COPY",BODY,{"derivedFrom":makeQuery(id+"F2.opPattern","COPY",BODY,{"derivedFrom":makeQuery(id+"F1.opRevolve","SWEPT_BODY",BODY,{"disambiguationData":[OSD([sQuery(id+"F0.wireOp",EDGE,"E1")])]}),"instanceName":"1"}),"instanceName":"1"}),"instanceName":"1"}),"instanceName":"1"}),"instanceName":"1"}),"instanceName":"1"}),"instanceName":"1"}),"instanceName":"1"}),"instanceName":"1"});
            var Q3050;
            Q3050=makeQuery(id+"F13.opPattern","COPY",BODY,{"derivedFrom":makeQuery(id+"F12.opPattern","COPY",BODY,{"derivedFrom":makeQuery(id+"F11.opPattern","COPY",BODY,{"derivedFrom":makeQuery(id+"F10.opPattern","COPY",BODY,{"derivedFrom":makeQuery(id+"F9.opPattern","COPY",BODY,{"derivedFrom":makeQuery(id+"F8.opPattern","COPY",BODY,{"derivedFrom":makeQuery(id+"F7.opPattern","COPY",BODY,{"derivedFrom":makeQuery(id+"F4.opPattern","COPY",BODY,{"derivedFrom":makeQuery(id+"F1.opRevolve","SWEPT_BODY",BODY,{"disambiguationData":[OSD([sQuery(id+"F0.wireOp",EDGE,"E1")])]}),"instanceName":"1"}),"instanceName":"1"}),"instanceName":"1"}),"instanceName":"1"}),"instanceName":"1"}),"instanceName":"1"}),"instanceName":"1"}),"instanceName":"1"});
            var Q3051;
            Q3051=makeQuery(id+"F13.opPattern","COPY",BODY,{"derivedFrom":makeQuery(id+"F12.opPattern","COPY",BODY,{"derivedFrom":makeQuery(id+"F11.opPattern","COPY",BODY,{"derivedFrom":makeQuery(id+"F10.opPattern","COPY",BODY,{"derivedFrom":makeQuery(id+"F9.opPattern","COPY",BODY,{"derivedFrom":makeQuery(id+"F8.opPattern","COPY",BODY,{"derivedFrom":makeQuery(id+"F7.opPattern","COPY",BODY,{"derivedFrom":makeQuery(id+"F4.opPattern","COPY",BODY,{"derivedFrom":makeQuery(id+"F2.opPattern","COPY",BODY,{"derivedFrom":makeQuery(id+"F1.opRevolve","SWEPT_BODY",BODY,{"disambiguationData":[OSD([sQuery(id+"F0.wireOp",EDGE,"E1")])]}),"instanceName":"1"}),"instanceName":"1"}),"instanceName":"1"}),"instanceName":"1"}),"instanceName":"1"}),"instanceName":"1"}),"instanceName":"1"}),"instanceName":"1"}),"instanceName":"1"});
            var Q3052;
            Q3052=makeQuery(id+"F13.opPattern","COPY",BODY,{"derivedFrom":makeQuery(id+"F12.opPattern","COPY",BODY,{"derivedFrom":makeQuery(id+"F11.opPattern","COPY",BODY,{"derivedFrom":makeQuery(id+"F10.opPattern","COPY",BODY,{"derivedFrom":makeQuery(id+"F9.opPattern","COPY",BODY,{"derivedFrom":makeQuery(id+"F8.opPattern","COPY",BODY,{"derivedFrom":makeQuery(id+"F7.opPattern","COPY",BODY,{"derivedFrom":makeQuery(id+"F4.opPattern","COPY",BODY,{"derivedFrom":makeQuery(id+"F3.opPattern","COPY",BODY,{"derivedFrom":makeQuery(id+"F2.opPattern","COPY",BODY,{"derivedFrom":makeQuery(id+"F1.opRevolve","SWEPT_BODY",BODY,{"disambiguationData":[OSD([sQuery(id+"F0.wireOp",EDGE,"E1")])]}),"instanceName":"1"}),"instanceName":"1"}),"instanceName":"1"}),"instanceName":"1"}),"instanceName":"1"}),"instanceName":"1"}),"instanceName":"1"}),"instanceName":"1"}),"instanceName":"1"}),"instanceName":"1"});
            var Q3053;
            Q3053=makeQuery(id+"F13.opPattern","COPY",BODY,{"derivedFrom":makeQuery(id+"F12.opPattern","COPY",BODY,{"derivedFrom":makeQuery(id+"F11.opPattern","COPY",BODY,{"derivedFrom":makeQuery(id+"F10.opPattern","COPY",BODY,{"derivedFrom":makeQuery(id+"F9.opPattern","COPY",BODY,{"derivedFrom":makeQuery(id+"F8.opPattern","COPY",BODY,{"derivedFrom":makeQuery(id+"F7.opPattern","COPY",BODY,{"derivedFrom":makeQuery(id+"F5.opPattern","COPY",BODY,{"derivedFrom":makeQuery(id+"F1.opRevolve","SWEPT_BODY",BODY,{"disambiguationData":[OSD([sQuery(id+"F0.wireOp",EDGE,"E1")])]}),"instanceName":"1"}),"instanceName":"1"}),"instanceName":"1"}),"instanceName":"1"}),"instanceName":"1"}),"instanceName":"1"}),"instanceName":"1"}),"instanceName":"1"});
            var Q3054;
            Q3054=makeQuery(id+"F13.opPattern","COPY",BODY,{"derivedFrom":makeQuery(id+"F12.opPattern","COPY",BODY,{"derivedFrom":makeQuery(id+"F11.opPattern","COPY",BODY,{"derivedFrom":makeQuery(id+"F10.opPattern","COPY",BODY,{"derivedFrom":makeQuery(id+"F9.opPattern","COPY",BODY,{"derivedFrom":makeQuery(id+"F8.opPattern","COPY",BODY,{"derivedFrom":makeQuery(id+"F7.opPattern","COPY",BODY,{"derivedFrom":makeQuery(id+"F5.opPattern","COPY",BODY,{"derivedFrom":makeQuery(id+"F2.opPattern","COPY",BODY,{"derivedFrom":makeQuery(id+"F1.opRevolve","SWEPT_BODY",BODY,{"disambiguationData":[OSD([sQuery(id+"F0.wireOp",EDGE,"E1")])]}),"instanceName":"1"}),"instanceName":"1"}),"instanceName":"1"}),"instanceName":"1"}),"instanceName":"1"}),"instanceName":"1"}),"instanceName":"1"}),"instanceName":"1"}),"instanceName":"1"});
            var Q3055;
            Q3055=makeQuery(id+"F13.opPattern","COPY",BODY,{"derivedFrom":makeQuery(id+"F12.opPattern","COPY",BODY,{"derivedFrom":makeQuery(id+"F11.opPattern","COPY",BODY,{"derivedFrom":makeQuery(id+"F10.opPattern","COPY",BODY,{"derivedFrom":makeQuery(id+"F9.opPattern","COPY",BODY,{"derivedFrom":makeQuery(id+"F8.opPattern","COPY",BODY,{"derivedFrom":makeQuery(id+"F7.opPattern","COPY",BODY,{"derivedFrom":makeQuery(id+"F5.opPattern","COPY",BODY,{"derivedFrom":makeQuery(id+"F3.opPattern","COPY",BODY,{"derivedFrom":makeQuery(id+"F2.opPattern","COPY",BODY,{"derivedFrom":makeQuery(id+"F1.opRevolve","SWEPT_BODY",BODY,{"disambiguationData":[OSD([sQuery(id+"F0.wireOp",EDGE,"E1")])]}),"instanceName":"1"}),"instanceName":"1"}),"instanceName":"1"}),"instanceName":"1"}),"instanceName":"1"}),"instanceName":"1"}),"instanceName":"1"}),"instanceName":"1"}),"instanceName":"1"}),"instanceName":"1"});
            var Q3056;
            Q3056=makeQuery(id+"F13.opPattern","COPY",BODY,{"derivedFrom":makeQuery(id+"F12.opPattern","COPY",BODY,{"derivedFrom":makeQuery(id+"F11.opPattern","COPY",BODY,{"derivedFrom":makeQuery(id+"F10.opPattern","COPY",BODY,{"derivedFrom":makeQuery(id+"F9.opPattern","COPY",BODY,{"derivedFrom":makeQuery(id+"F8.opPattern","COPY",BODY,{"derivedFrom":makeQuery(id+"F7.opPattern","COPY",BODY,{"derivedFrom":makeQuery(id+"F5.opPattern","COPY",BODY,{"derivedFrom":makeQuery(id+"F4.opPattern","COPY",BODY,{"derivedFrom":makeQuery(id+"F1.opRevolve","SWEPT_BODY",BODY,{"disambiguationData":[OSD([sQuery(id+"F0.wireOp",EDGE,"E1")])]}),"instanceName":"1"}),"instanceName":"1"}),"instanceName":"1"}),"instanceName":"1"}),"instanceName":"1"}),"instanceName":"1"}),"instanceName":"1"}),"instanceName":"1"}),"instanceName":"1"});
            var Q3057;
            Q3057=makeQuery(id+"F13.opPattern","COPY",BODY,{"derivedFrom":makeQuery(id+"F12.opPattern","COPY",BODY,{"derivedFrom":makeQuery(id+"F11.opPattern","COPY",BODY,{"derivedFrom":makeQuery(id+"F10.opPattern","COPY",BODY,{"derivedFrom":makeQuery(id+"F9.opPattern","COPY",BODY,{"derivedFrom":makeQuery(id+"F8.opPattern","COPY",BODY,{"derivedFrom":makeQuery(id+"F7.opPattern","COPY",BODY,{"derivedFrom":makeQuery(id+"F5.opPattern","COPY",BODY,{"derivedFrom":makeQuery(id+"F4.opPattern","COPY",BODY,{"derivedFrom":makeQuery(id+"F2.opPattern","COPY",BODY,{"derivedFrom":makeQuery(id+"F1.opRevolve","SWEPT_BODY",BODY,{"disambiguationData":[OSD([sQuery(id+"F0.wireOp",EDGE,"E1")])]}),"instanceName":"1"}),"instanceName":"1"}),"instanceName":"1"}),"instanceName":"1"}),"instanceName":"1"}),"instanceName":"1"}),"instanceName":"1"}),"instanceName":"1"}),"instanceName":"1"}),"instanceName":"1"});
            var Q3058;
            Q3058=makeQuery(id+"F13.opPattern","COPY",BODY,{"derivedFrom":makeQuery(id+"F12.opPattern","COPY",BODY,{"derivedFrom":makeQuery(id+"F11.opPattern","COPY",BODY,{"derivedFrom":makeQuery(id+"F10.opPattern","COPY",BODY,{"derivedFrom":makeQuery(id+"F9.opPattern","COPY",BODY,{"derivedFrom":makeQuery(id+"F8.opPattern","COPY",BODY,{"derivedFrom":makeQuery(id+"F7.opPattern","COPY",BODY,{"derivedFrom":makeQuery(id+"F5.opPattern","COPY",BODY,{"derivedFrom":makeQuery(id+"F4.opPattern","COPY",BODY,{"derivedFrom":makeQuery(id+"F3.opPattern","COPY",BODY,{"derivedFrom":makeQuery(id+"F2.opPattern","COPY",BODY,{"derivedFrom":makeQuery(id+"F1.opRevolve","SWEPT_BODY",BODY,{"disambiguationData":[OSD([sQuery(id+"F0.wireOp",EDGE,"E1")])]}),"instanceName":"1"}),"instanceName":"1"}),"instanceName":"1"}),"instanceName":"1"}),"instanceName":"1"}),"instanceName":"1"}),"instanceName":"1"}),"instanceName":"1"}),"instanceName":"1"}),"instanceName":"1"}),"instanceName":"1"});
            var Q3059;
            Q3059=makeQuery(id+"F13.opPattern","COPY",BODY,{"derivedFrom":makeQuery(id+"F12.opPattern","COPY",BODY,{"derivedFrom":makeQuery(id+"F11.opPattern","COPY",BODY,{"derivedFrom":makeQuery(id+"F10.opPattern","COPY",BODY,{"derivedFrom":makeQuery(id+"F9.opPattern","COPY",BODY,{"derivedFrom":makeQuery(id+"F8.opPattern","COPY",BODY,{"derivedFrom":makeQuery(id+"F7.opPattern","COPY",BODY,{"derivedFrom":makeQuery(id+"F6.opPattern","COPY",BODY,{"derivedFrom":makeQuery(id+"F1.opRevolve","SWEPT_BODY",BODY,{"disambiguationData":[OSD([sQuery(id+"F0.wireOp",EDGE,"E1")])]}),"instanceName":"1"}),"instanceName":"1"}),"instanceName":"1"}),"instanceName":"1"}),"instanceName":"1"}),"instanceName":"1"}),"instanceName":"1"}),"instanceName":"1"});
            var Q3060;
            Q3060=makeQuery(id+"F13.opPattern","COPY",BODY,{"derivedFrom":makeQuery(id+"F12.opPattern","COPY",BODY,{"derivedFrom":makeQuery(id+"F11.opPattern","COPY",BODY,{"derivedFrom":makeQuery(id+"F10.opPattern","COPY",BODY,{"derivedFrom":makeQuery(id+"F9.opPattern","COPY",BODY,{"derivedFrom":makeQuery(id+"F8.opPattern","COPY",BODY,{"derivedFrom":makeQuery(id+"F7.opPattern","COPY",BODY,{"derivedFrom":makeQuery(id+"F6.opPattern","COPY",BODY,{"derivedFrom":makeQuery(id+"F2.opPattern","COPY",BODY,{"derivedFrom":makeQuery(id+"F1.opRevolve","SWEPT_BODY",BODY,{"disambiguationData":[OSD([sQuery(id+"F0.wireOp",EDGE,"E1")])]}),"instanceName":"1"}),"instanceName":"1"}),"instanceName":"1"}),"instanceName":"1"}),"instanceName":"1"}),"instanceName":"1"}),"instanceName":"1"}),"instanceName":"1"}),"instanceName":"1"});
            var Q3061;
            Q3061=makeQuery(id+"F13.opPattern","COPY",BODY,{"derivedFrom":makeQuery(id+"F12.opPattern","COPY",BODY,{"derivedFrom":makeQuery(id+"F11.opPattern","COPY",BODY,{"derivedFrom":makeQuery(id+"F10.opPattern","COPY",BODY,{"derivedFrom":makeQuery(id+"F9.opPattern","COPY",BODY,{"derivedFrom":makeQuery(id+"F8.opPattern","COPY",BODY,{"derivedFrom":makeQuery(id+"F7.opPattern","COPY",BODY,{"derivedFrom":makeQuery(id+"F6.opPattern","COPY",BODY,{"derivedFrom":makeQuery(id+"F3.opPattern","COPY",BODY,{"derivedFrom":makeQuery(id+"F2.opPattern","COPY",BODY,{"derivedFrom":makeQuery(id+"F1.opRevolve","SWEPT_BODY",BODY,{"disambiguationData":[OSD([sQuery(id+"F0.wireOp",EDGE,"E1")])]}),"instanceName":"1"}),"instanceName":"1"}),"instanceName":"1"}),"instanceName":"1"}),"instanceName":"1"}),"instanceName":"1"}),"instanceName":"1"}),"instanceName":"1"}),"instanceName":"1"}),"instanceName":"1"});
            var Q3062;
            Q3062=makeQuery(id+"F13.opPattern","COPY",BODY,{"derivedFrom":makeQuery(id+"F12.opPattern","COPY",BODY,{"derivedFrom":makeQuery(id+"F11.opPattern","COPY",BODY,{"derivedFrom":makeQuery(id+"F10.opPattern","COPY",BODY,{"derivedFrom":makeQuery(id+"F9.opPattern","COPY",BODY,{"derivedFrom":makeQuery(id+"F8.opPattern","COPY",BODY,{"derivedFrom":makeQuery(id+"F7.opPattern","COPY",BODY,{"derivedFrom":makeQuery(id+"F6.opPattern","COPY",BODY,{"derivedFrom":makeQuery(id+"F4.opPattern","COPY",BODY,{"derivedFrom":makeQuery(id+"F1.opRevolve","SWEPT_BODY",BODY,{"disambiguationData":[OSD([sQuery(id+"F0.wireOp",EDGE,"E1")])]}),"instanceName":"1"}),"instanceName":"1"}),"instanceName":"1"}),"instanceName":"1"}),"instanceName":"1"}),"instanceName":"1"}),"instanceName":"1"}),"instanceName":"1"}),"instanceName":"1"});
            var Q3063;
            Q3063=makeQuery(id+"F13.opPattern","COPY",BODY,{"derivedFrom":makeQuery(id+"F12.opPattern","COPY",BODY,{"derivedFrom":makeQuery(id+"F11.opPattern","COPY",BODY,{"derivedFrom":makeQuery(id+"F10.opPattern","COPY",BODY,{"derivedFrom":makeQuery(id+"F9.opPattern","COPY",BODY,{"derivedFrom":makeQuery(id+"F8.opPattern","COPY",BODY,{"derivedFrom":makeQuery(id+"F7.opPattern","COPY",BODY,{"derivedFrom":makeQuery(id+"F6.opPattern","COPY",BODY,{"derivedFrom":makeQuery(id+"F4.opPattern","COPY",BODY,{"derivedFrom":makeQuery(id+"F2.opPattern","COPY",BODY,{"derivedFrom":makeQuery(id+"F1.opRevolve","SWEPT_BODY",BODY,{"disambiguationData":[OSD([sQuery(id+"F0.wireOp",EDGE,"E1")])]}),"instanceName":"1"}),"instanceName":"1"}),"instanceName":"1"}),"instanceName":"1"}),"instanceName":"1"}),"instanceName":"1"}),"instanceName":"1"}),"instanceName":"1"}),"instanceName":"1"}),"instanceName":"1"});
            var Q3064;
            Q3064=makeQuery(id+"F13.opPattern","COPY",BODY,{"derivedFrom":makeQuery(id+"F12.opPattern","COPY",BODY,{"derivedFrom":makeQuery(id+"F11.opPattern","COPY",BODY,{"derivedFrom":makeQuery(id+"F10.opPattern","COPY",BODY,{"derivedFrom":makeQuery(id+"F9.opPattern","COPY",BODY,{"derivedFrom":makeQuery(id+"F8.opPattern","COPY",BODY,{"derivedFrom":makeQuery(id+"F7.opPattern","COPY",BODY,{"derivedFrom":makeQuery(id+"F6.opPattern","COPY",BODY,{"derivedFrom":makeQuery(id+"F4.opPattern","COPY",BODY,{"derivedFrom":makeQuery(id+"F3.opPattern","COPY",BODY,{"derivedFrom":makeQuery(id+"F2.opPattern","COPY",BODY,{"derivedFrom":makeQuery(id+"F1.opRevolve","SWEPT_BODY",BODY,{"disambiguationData":[OSD([sQuery(id+"F0.wireOp",EDGE,"E1")])]}),"instanceName":"1"}),"instanceName":"1"}),"instanceName":"1"}),"instanceName":"1"}),"instanceName":"1"}),"instanceName":"1"}),"instanceName":"1"}),"instanceName":"1"}),"instanceName":"1"}),"instanceName":"1"}),"instanceName":"1"});
            var Q3065;
            Q3065=makeQuery(id+"F13.opPattern","COPY",BODY,{"derivedFrom":makeQuery(id+"F12.opPattern","COPY",BODY,{"derivedFrom":makeQuery(id+"F11.opPattern","COPY",BODY,{"derivedFrom":makeQuery(id+"F10.opPattern","COPY",BODY,{"derivedFrom":makeQuery(id+"F9.opPattern","COPY",BODY,{"derivedFrom":makeQuery(id+"F8.opPattern","COPY",BODY,{"derivedFrom":makeQuery(id+"F7.opPattern","COPY",BODY,{"derivedFrom":makeQuery(id+"F6.opPattern","COPY",BODY,{"derivedFrom":makeQuery(id+"F5.opPattern","COPY",BODY,{"derivedFrom":makeQuery(id+"F1.opRevolve","SWEPT_BODY",BODY,{"disambiguationData":[OSD([sQuery(id+"F0.wireOp",EDGE,"E1")])]}),"instanceName":"1"}),"instanceName":"1"}),"instanceName":"1"}),"instanceName":"1"}),"instanceName":"1"}),"instanceName":"1"}),"instanceName":"1"}),"instanceName":"1"}),"instanceName":"1"});
            var Q3066;
            Q3066=makeQuery(id+"F13.opPattern","COPY",BODY,{"derivedFrom":makeQuery(id+"F12.opPattern","COPY",BODY,{"derivedFrom":makeQuery(id+"F11.opPattern","COPY",BODY,{"derivedFrom":makeQuery(id+"F10.opPattern","COPY",BODY,{"derivedFrom":makeQuery(id+"F9.opPattern","COPY",BODY,{"derivedFrom":makeQuery(id+"F8.opPattern","COPY",BODY,{"derivedFrom":makeQuery(id+"F7.opPattern","COPY",BODY,{"derivedFrom":makeQuery(id+"F6.opPattern","COPY",BODY,{"derivedFrom":makeQuery(id+"F5.opPattern","COPY",BODY,{"derivedFrom":makeQuery(id+"F2.opPattern","COPY",BODY,{"derivedFrom":makeQuery(id+"F1.opRevolve","SWEPT_BODY",BODY,{"disambiguationData":[OSD([sQuery(id+"F0.wireOp",EDGE,"E1")])]}),"instanceName":"1"}),"instanceName":"1"}),"instanceName":"1"}),"instanceName":"1"}),"instanceName":"1"}),"instanceName":"1"}),"instanceName":"1"}),"instanceName":"1"}),"instanceName":"1"}),"instanceName":"1"});
            var Q3067;
            Q3067=makeQuery(id+"F13.opPattern","COPY",BODY,{"derivedFrom":makeQuery(id+"F12.opPattern","COPY",BODY,{"derivedFrom":makeQuery(id+"F11.opPattern","COPY",BODY,{"derivedFrom":makeQuery(id+"F10.opPattern","COPY",BODY,{"derivedFrom":makeQuery(id+"F9.opPattern","COPY",BODY,{"derivedFrom":makeQuery(id+"F8.opPattern","COPY",BODY,{"derivedFrom":makeQuery(id+"F7.opPattern","COPY",BODY,{"derivedFrom":makeQuery(id+"F6.opPattern","COPY",BODY,{"derivedFrom":makeQuery(id+"F5.opPattern","COPY",BODY,{"derivedFrom":makeQuery(id+"F3.opPattern","COPY",BODY,{"derivedFrom":makeQuery(id+"F2.opPattern","COPY",BODY,{"derivedFrom":makeQuery(id+"F1.opRevolve","SWEPT_BODY",BODY,{"disambiguationData":[OSD([sQuery(id+"F0.wireOp",EDGE,"E1")])]}),"instanceName":"1"}),"instanceName":"1"}),"instanceName":"1"}),"instanceName":"1"}),"instanceName":"1"}),"instanceName":"1"}),"instanceName":"1"}),"instanceName":"1"}),"instanceName":"1"}),"instanceName":"1"}),"instanceName":"1"});
            var Q3068;
            Q3068=makeQuery(id+"F13.opPattern","COPY",BODY,{"derivedFrom":makeQuery(id+"F12.opPattern","COPY",BODY,{"derivedFrom":makeQuery(id+"F11.opPattern","COPY",BODY,{"derivedFrom":makeQuery(id+"F10.opPattern","COPY",BODY,{"derivedFrom":makeQuery(id+"F9.opPattern","COPY",BODY,{"derivedFrom":makeQuery(id+"F8.opPattern","COPY",BODY,{"derivedFrom":makeQuery(id+"F7.opPattern","COPY",BODY,{"derivedFrom":makeQuery(id+"F6.opPattern","COPY",BODY,{"derivedFrom":makeQuery(id+"F5.opPattern","COPY",BODY,{"derivedFrom":makeQuery(id+"F4.opPattern","COPY",BODY,{"derivedFrom":makeQuery(id+"F1.opRevolve","SWEPT_BODY",BODY,{"disambiguationData":[OSD([sQuery(id+"F0.wireOp",EDGE,"E1")])]}),"instanceName":"1"}),"instanceName":"1"}),"instanceName":"1"}),"instanceName":"1"}),"instanceName":"1"}),"instanceName":"1"}),"instanceName":"1"}),"instanceName":"1"}),"instanceName":"1"}),"instanceName":"1"});
            var Q3069;
            Q3069=makeQuery(id+"F13.opPattern","COPY",BODY,{"derivedFrom":makeQuery(id+"F12.opPattern","COPY",BODY,{"derivedFrom":makeQuery(id+"F11.opPattern","COPY",BODY,{"derivedFrom":makeQuery(id+"F10.opPattern","COPY",BODY,{"derivedFrom":makeQuery(id+"F9.opPattern","COPY",BODY,{"derivedFrom":makeQuery(id+"F8.opPattern","COPY",BODY,{"derivedFrom":makeQuery(id+"F7.opPattern","COPY",BODY,{"derivedFrom":makeQuery(id+"F6.opPattern","COPY",BODY,{"derivedFrom":makeQuery(id+"F5.opPattern","COPY",BODY,{"derivedFrom":makeQuery(id+"F4.opPattern","COPY",BODY,{"derivedFrom":makeQuery(id+"F2.opPattern","COPY",BODY,{"derivedFrom":makeQuery(id+"F1.opRevolve","SWEPT_BODY",BODY,{"disambiguationData":[OSD([sQuery(id+"F0.wireOp",EDGE,"E1")])]}),"instanceName":"1"}),"instanceName":"1"}),"instanceName":"1"}),"instanceName":"1"}),"instanceName":"1"}),"instanceName":"1"}),"instanceName":"1"}),"instanceName":"1"}),"instanceName":"1"}),"instanceName":"1"}),"instanceName":"1"});
            var Q3070;
            Q3070=makeQuery(id+"F13.opPattern","COPY",BODY,{"derivedFrom":makeQuery(id+"F12.opPattern","COPY",BODY,{"derivedFrom":makeQuery(id+"F11.opPattern","COPY",BODY,{"derivedFrom":makeQuery(id+"F10.opPattern","COPY",BODY,{"derivedFrom":makeQuery(id+"F9.opPattern","COPY",BODY,{"derivedFrom":makeQuery(id+"F8.opPattern","COPY",BODY,{"derivedFrom":makeQuery(id+"F7.opPattern","COPY",BODY,{"derivedFrom":makeQuery(id+"F6.opPattern","COPY",BODY,{"derivedFrom":makeQuery(id+"F5.opPattern","COPY",BODY,{"derivedFrom":makeQuery(id+"F4.opPattern","COPY",BODY,{"derivedFrom":makeQuery(id+"F3.opPattern","COPY",BODY,{"derivedFrom":makeQuery(id+"F2.opPattern","COPY",BODY,{"derivedFrom":makeQuery(id+"F1.opRevolve","SWEPT_BODY",BODY,{"disambiguationData":[OSD([sQuery(id+"F0.wireOp",EDGE,"E1")])]}),"instanceName":"1"}),"instanceName":"1"}),"instanceName":"1"}),"instanceName":"1"}),"instanceName":"1"}),"instanceName":"1"}),"instanceName":"1"}),"instanceName":"1"}),"instanceName":"1"}),"instanceName":"1"}),"instanceName":"1"}),"instanceName":"1"});
            var Q3071;
            Q3071=makeQuery(id+"F1.opRevolve","SWEPT_BODY",BODY,{"disambiguationData":[OSD([sQuery(id+"F0.wireOp",EDGE,"E1")])]});
            transform(context, id + "F14", {"entities" : qUnion([Q0, Q1, Q2, Q3, Q4, Q5, Q6, Q7, Q8, Q9, Q10, Q11, Q12, Q13, Q14, Q15, Q16, Q17, Q18, Q19, Q20, Q21, Q22, Q23, Q24, Q25, Q26, Q27, Q28, Q29, Q30, Q31, Q32, Q33, Q34, Q35, Q36, Q37, Q38, Q39, Q40, Q41, Q42, Q43, Q44, Q45, Q46, Q47, Q48, Q49, Q50, Q51, Q52, Q53, Q54, Q55, Q56, Q57, Q58, Q59, Q60, Q61, Q62, Q63, Q64, Q65, Q66, Q67, Q68, Q69, Q70, Q71, Q72, Q73, Q74, Q75, Q76, Q77, Q78, Q79, Q80, Q81, Q82, Q83, Q84, Q85, Q86, Q87, Q88, Q89, Q90, Q91, Q92, Q93, Q94, Q95, Q96, Q97, Q98, Q99, Q100, Q101, Q102, Q103, Q104, Q105, Q106, Q107, Q108, Q109, Q110, Q111, Q112, Q113, Q114, Q115, Q116, Q117, Q118, Q119, Q120, Q121, Q122, Q123, Q124, Q125, Q126, Q127, Q128, Q129, Q130, Q131, Q132, Q133, Q134, Q135, Q136, Q137, Q138, Q139, Q140, Q141, Q142, Q143, Q144, Q145, Q146, Q147, Q148, Q149, Q150, Q151, Q152, Q153, Q154, Q155, Q156, Q157, Q158, Q159, Q160, Q161, Q162, Q163, Q164, Q165, Q166, Q167, Q168, Q169, Q170, Q171, Q172, Q173, Q174, Q175, Q176, Q177, Q178, Q179, Q180, Q181, Q182, Q183, Q184, Q185, Q186, Q187, Q188, Q189, Q190, Q191, Q192, Q193, Q194, Q195, Q196, Q197, Q198, Q199, Q200, Q201, Q202, Q203, Q204, Q205, Q206, Q207, Q208, Q209, Q210, Q211, Q212, Q213, Q214, Q215, Q216, Q217, Q218, Q219, Q220, Q221, Q222, Q223, Q224, Q225, Q226, Q227, Q228, Q229, Q230, Q231, Q232, Q233, Q234, Q235, Q236, Q237, Q238, Q239, Q240, Q241, Q242, Q243, Q244, Q245, Q246, Q247, Q248, Q249, Q250, Q251, Q252, Q253, Q254, Q255, Q256, Q257, Q258, Q259, Q260, Q261, Q262, Q263, Q264, Q265, Q266, Q267, Q268, Q269, Q270, Q271, Q272, Q273, Q274, Q275, Q276, Q277, Q278, Q279, Q280, Q281, Q282, Q283, Q284, Q285, Q286, Q287, Q288, Q289, Q290, Q291, Q292, Q293, Q294, Q295, Q296, Q297, Q298, Q299, Q300, Q301, Q302, Q303, Q304, Q305, Q306, Q307, Q308, Q309, Q310, Q311, Q312, Q313, Q314, Q315, Q316, Q317, Q318, Q319, Q320, Q321, Q322, Q323, Q324, Q325, Q326, Q327, Q328, Q329, Q330, Q331, Q332, Q333, Q334, Q335, Q336, Q337, Q338, Q339, Q340, Q341, Q342, Q343, Q344, Q345, Q346, Q347, Q348, Q349, Q350, Q351, Q352, Q353, Q354, Q355, Q356, Q357, Q358, Q359, Q360, Q361, Q362, Q363, Q364, Q365, Q366, Q367, Q368, Q369, Q370, Q371, Q372, Q373, Q374, Q375, Q376, Q377, Q378, Q379, Q380, Q381, Q382, Q383, Q384, Q385, Q386, Q387, Q388, Q389, Q390, Q391, Q392, Q393, Q394, Q395, Q396, Q397, Q398, Q399, Q400, Q401, Q402, Q403, Q404, Q405, Q406, Q407, Q408, Q409, Q410, Q411, Q412, Q413, Q414, Q415, Q416, Q417, Q418, Q419, Q420, Q421, Q422, Q423, Q424, Q425, Q426, Q427, Q428, Q429, Q430, Q431, Q432, Q433, Q434, Q435, Q436, Q437, Q438, Q439, Q440, Q441, Q442, Q443, Q444, Q445, Q446, Q447, Q448, Q449, Q450, Q451, Q452, Q453, Q454, Q455, Q456, Q457, Q458, Q459, Q460, Q461, Q462, Q463, Q464, Q465, Q466, Q467, Q468, Q469, Q470, Q471, Q472, Q473, Q474, Q475, Q476, Q477, Q478, Q479, Q480, Q481, Q482, Q483, Q484, Q485, Q486, Q487, Q488, Q489, Q490, Q491, Q492, Q493, Q494, Q495, Q496, Q497, Q498, Q499, Q500, Q501, Q502, Q503, Q504, Q505, Q506, Q507, Q508, Q509, Q510, Q511, Q512, Q513, Q514, Q515, Q516, Q517, Q518, Q519, Q520, Q521, Q522, Q523, Q524, Q525, Q526, Q527, Q528, Q529, Q530, Q531, Q532, Q533, Q534, Q535, Q536, Q537, Q538, Q539, Q540, Q541, Q542, Q543, Q544, Q545, Q546, Q547, Q548, Q549, Q550, Q551, Q552, Q553, Q554, Q555, Q556, Q557, Q558, Q559, Q560, Q561, Q562, Q563, Q564, Q565, Q566, Q567, Q568, Q569, Q570, Q571, Q572, Q573, Q574, Q575, Q576, Q577, Q578, Q579, Q580, Q581, Q582, Q583, Q584, Q585, Q586, Q587, Q588, Q589, Q590, Q591, Q592, Q593, Q594, Q595, Q596, Q597, Q598, Q599, Q600, Q601, Q602, Q603, Q604, Q605, Q606, Q607, Q608, Q609, Q610, Q611, Q612, Q613, Q614, Q615, Q616, Q617, Q618, Q619, Q620, Q621, Q622, Q623, Q624, Q625, Q626, Q627, Q628, Q629, Q630, Q631, Q632, Q633, Q634, Q635, Q636, Q637, Q638, Q639, Q640, Q641, Q642, Q643, Q644, Q645, Q646, Q647, Q648, Q649, Q650, Q651, Q652, Q653, Q654, Q655, Q656, Q657, Q658, Q659, Q660, Q661, Q662, Q663, Q664, Q665, Q666, Q667, Q668, Q669, Q670, Q671, Q672, Q673, Q674, Q675, Q676, Q677, Q678, Q679, Q680, Q681, Q682, Q683, Q684, Q685, Q686, Q687, Q688, Q689, Q690, Q691, Q692, Q693, Q694, Q695, Q696, Q697, Q698, Q699, Q700, Q701, Q702, Q703, Q704, Q705, Q706, Q707, Q708, Q709, Q710, Q711, Q712, Q713, Q714, Q715, Q716, Q717, Q718, Q719, Q720, Q721, Q722, Q723, Q724, Q725, Q726, Q727, Q728, Q729, Q730, Q731, Q732, Q733, Q734, Q735, Q736, Q737, Q738, Q739, Q740, Q741, Q742, Q743, Q744, Q745, Q746, Q747, Q748, Q749, Q750, Q751, Q752, Q753, Q754, Q755, Q756, Q757, Q758, Q759, Q760, Q761, Q762, Q763, Q764, Q765, Q766, Q767, Q768, Q769, Q770, Q771, Q772, Q773, Q774, Q775, Q776, Q777, Q778, Q779, Q780, Q781, Q782, Q783, Q784, Q785, Q786, Q787, Q788, Q789, Q790, Q791, Q792, Q793, Q794, Q795, Q796, Q797, Q798, Q799, Q800, Q801, Q802, Q803, Q804, Q805, Q806, Q807, Q808, Q809, Q810, Q811, Q812, Q813, Q814, Q815, Q816, Q817, Q818, Q819, Q820, Q821, Q822, Q823, Q824, Q825, Q826, Q827, Q828, Q829, Q830, Q831, Q832, Q833, Q834, Q835, Q836, Q837, Q838, Q839, Q840, Q841, Q842, Q843, Q844, Q845, Q846, Q847, Q848, Q849, Q850, Q851, Q852, Q853, Q854, Q855, Q856, Q857, Q858, Q859, Q860, Q861, Q862, Q863, Q864, Q865, Q866, Q867, Q868, Q869, Q870, Q871, Q872, Q873, Q874, Q875, Q876, Q877, Q878, Q879, Q880, Q881, Q882, Q883, Q884, Q885, Q886, Q887, Q888, Q889, Q890, Q891, Q892, Q893, Q894, Q895, Q896, Q897, Q898, Q899, Q900, Q901, Q902, Q903, Q904, Q905, Q906, Q907, Q908, Q909, Q910, Q911, Q912, Q913, Q914, Q915, Q916, Q917, Q918, Q919, Q920, Q921, Q922, Q923, Q924, Q925, Q926, Q927, Q928, Q929, Q930, Q931, Q932, Q933, Q934, Q935, Q936, Q937, Q938, Q939, Q940, Q941, Q942, Q943, Q944, Q945, Q946, Q947, Q948, Q949, Q950, Q951, Q952, Q953, Q954, Q955, Q956, Q957, Q958, Q959, Q960, Q961, Q962, Q963, Q964, Q965, Q966, Q967, Q968, Q969, Q970, Q971, Q972, Q973, Q974, Q975, Q976, Q977, Q978, Q979, Q980, Q981, Q982, Q983, Q984, Q985, Q986, Q987, Q988, Q989, Q990, Q991, Q992, Q993, Q994, Q995, Q996, Q997, Q998, Q999, Q1000, Q1001, Q1002, Q1003, Q1004, Q1005, Q1006, Q1007, Q1008, Q1009, Q1010, Q1011, Q1012, Q1013, Q1014, Q1015, Q1016, Q1017, Q1018, Q1019, Q1020, Q1021, Q1022, Q1023, Q1024, Q1025, Q1026, Q1027, Q1028, Q1029, Q1030, Q1031, Q1032, Q1033, Q1034, Q1035, Q1036, Q1037, Q1038, Q1039, Q1040, Q1041, Q1042, Q1043, Q1044, Q1045, Q1046, Q1047, Q1048, Q1049, Q1050, Q1051, Q1052, Q1053, Q1054, Q1055, Q1056, Q1057, Q1058, Q1059, Q1060, Q1061, Q1062, Q1063, Q1064, Q1065, Q1066, Q1067, Q1068, Q1069, Q1070, Q1071, Q1072, Q1073, Q1074, Q1075, Q1076, Q1077, Q1078, Q1079, Q1080, Q1081, Q1082, Q1083, Q1084, Q1085, Q1086, Q1087, Q1088, Q1089, Q1090, Q1091, Q1092, Q1093, Q1094, Q1095, Q1096, Q1097, Q1098, Q1099, Q1100, Q1101, Q1102, Q1103, Q1104, Q1105, Q1106, Q1107, Q1108, Q1109, Q1110, Q1111, Q1112, Q1113, Q1114, Q1115, Q1116, Q1117, Q1118, Q1119, Q1120, Q1121, Q1122, Q1123, Q1124, Q1125, Q1126, Q1127, Q1128, Q1129, Q1130, Q1131, Q1132, Q1133, Q1134, Q1135, Q1136, Q1137, Q1138, Q1139, Q1140, Q1141, Q1142, Q1143, Q1144, Q1145, Q1146, Q1147, Q1148, Q1149, Q1150, Q1151, Q1152, Q1153, Q1154, Q1155, Q1156, Q1157, Q1158, Q1159, Q1160, Q1161, Q1162, Q1163, Q1164, Q1165, Q1166, Q1167, Q1168, Q1169, Q1170, Q1171, Q1172, Q1173, Q1174, Q1175, Q1176, Q1177, Q1178, Q1179, Q1180, Q1181, Q1182, Q1183, Q1184, Q1185, Q1186, Q1187, Q1188, Q1189, Q1190, Q1191, Q1192, Q1193, Q1194, Q1195, Q1196, Q1197, Q1198, Q1199, Q1200, Q1201, Q1202, Q1203, Q1204, Q1205, Q1206, Q1207, Q1208, Q1209, Q1210, Q1211, Q1212, Q1213, Q1214, Q1215, Q1216, Q1217, Q1218, Q1219, Q1220, Q1221, Q1222, Q1223, Q1224, Q1225, Q1226, Q1227, Q1228, Q1229, Q1230, Q1231, Q1232, Q1233, Q1234, Q1235, Q1236, Q1237, Q1238, Q1239, Q1240, Q1241, Q1242, Q1243, Q1244, Q1245, Q1246, Q1247, Q1248, Q1249, Q1250, Q1251, Q1252, Q1253, Q1254, Q1255, Q1256, Q1257, Q1258, Q1259, Q1260, Q1261, Q1262, Q1263, Q1264, Q1265, Q1266, Q1267, Q1268, Q1269, Q1270, Q1271, Q1272, Q1273, Q1274, Q1275, Q1276, Q1277, Q1278, Q1279, Q1280, Q1281, Q1282, Q1283, Q1284, Q1285, Q1286, Q1287, Q1288, Q1289, Q1290, Q1291, Q1292, Q1293, Q1294, Q1295, Q1296, Q1297, Q1298, Q1299, Q1300, Q1301, Q1302, Q1303, Q1304, Q1305, Q1306, Q1307, Q1308, Q1309, Q1310, Q1311, Q1312, Q1313, Q1314, Q1315, Q1316, Q1317, Q1318, Q1319, Q1320, Q1321, Q1322, Q1323, Q1324, Q1325, Q1326, Q1327, Q1328, Q1329, Q1330, Q1331, Q1332, Q1333, Q1334, Q1335, Q1336, Q1337, Q1338, Q1339, Q1340, Q1341, Q1342, Q1343, Q1344, Q1345, Q1346, Q1347, Q1348, Q1349, Q1350, Q1351, Q1352, Q1353, Q1354, Q1355, Q1356, Q1357, Q1358, Q1359, Q1360, Q1361, Q1362, Q1363, Q1364, Q1365, Q1366, Q1367, Q1368, Q1369, Q1370, Q1371, Q1372, Q1373, Q1374, Q1375, Q1376, Q1377, Q1378, Q1379, Q1380, Q1381, Q1382, Q1383, Q1384, Q1385, Q1386, Q1387, Q1388, Q1389, Q1390, Q1391, Q1392, Q1393, Q1394, Q1395, Q1396, Q1397, Q1398, Q1399, Q1400, Q1401, Q1402, Q1403, Q1404, Q1405, Q1406, Q1407, Q1408, Q1409, Q1410, Q1411, Q1412, Q1413, Q1414, Q1415, Q1416, Q1417, Q1418, Q1419, Q1420, Q1421, Q1422, Q1423, Q1424, Q1425, Q1426, Q1427, Q1428, Q1429, Q1430, Q1431, Q1432, Q1433, Q1434, Q1435, Q1436, Q1437, Q1438, Q1439, Q1440, Q1441, Q1442, Q1443, Q1444, Q1445, Q1446, Q1447, Q1448, Q1449, Q1450, Q1451, Q1452, Q1453, Q1454, Q1455, Q1456, Q1457, Q1458, Q1459, Q1460, Q1461, Q1462, Q1463, Q1464, Q1465, Q1466, Q1467, Q1468, Q1469, Q1470, Q1471, Q1472, Q1473, Q1474, Q1475, Q1476, Q1477, Q1478, Q1479, Q1480, Q1481, Q1482, Q1483, Q1484, Q1485, Q1486, Q1487, Q1488, Q1489, Q1490, Q1491, Q1492, Q1493, Q1494, Q1495, Q1496, Q1497, Q1498, Q1499, Q1500, Q1501, Q1502, Q1503, Q1504, Q1505, Q1506, Q1507, Q1508, Q1509, Q1510, Q1511, Q1512, Q1513, Q1514, Q1515, Q1516, Q1517, Q1518, Q1519, Q1520, Q1521, Q1522, Q1523, Q1524, Q1525, Q1526, Q1527, Q1528, Q1529, Q1530, Q1531, Q1532, Q1533, Q1534, Q1535, Q1536, Q1537, Q1538, Q1539, Q1540, Q1541, Q1542, Q1543, Q1544, Q1545, Q1546, Q1547, Q1548, Q1549, Q1550, Q1551, Q1552, Q1553, Q1554, Q1555, Q1556, Q1557, Q1558, Q1559, Q1560, Q1561, Q1562, Q1563, Q1564, Q1565, Q1566, Q1567, Q1568, Q1569, Q1570, Q1571, Q1572, Q1573, Q1574, Q1575, Q1576, Q1577, Q1578, Q1579, Q1580, Q1581, Q1582, Q1583, Q1584, Q1585, Q1586, Q1587, Q1588, Q1589, Q1590, Q1591, Q1592, Q1593, Q1594, Q1595, Q1596, Q1597, Q1598, Q1599, Q1600, Q1601, Q1602, Q1603, Q1604, Q1605, Q1606, Q1607, Q1608, Q1609, Q1610, Q1611, Q1612, Q1613, Q1614, Q1615, Q1616, Q1617, Q1618, Q1619, Q1620, Q1621, Q1622, Q1623, Q1624, Q1625, Q1626, Q1627, Q1628, Q1629, Q1630, Q1631, Q1632, Q1633, Q1634, Q1635, Q1636, Q1637, Q1638, Q1639, Q1640, Q1641, Q1642, Q1643, Q1644, Q1645, Q1646, Q1647, Q1648, Q1649, Q1650, Q1651, Q1652, Q1653, Q1654, Q1655, Q1656, Q1657, Q1658, Q1659, Q1660, Q1661, Q1662, Q1663, Q1664, Q1665, Q1666, Q1667, Q1668, Q1669, Q1670, Q1671, Q1672, Q1673, Q1674, Q1675, Q1676, Q1677, Q1678, Q1679, Q1680, Q1681, Q1682, Q1683, Q1684, Q1685, Q1686, Q1687, Q1688, Q1689, Q1690, Q1691, Q1692, Q1693, Q1694, Q1695, Q1696, Q1697, Q1698, Q1699, Q1700, Q1701, Q1702, Q1703, Q1704, Q1705, Q1706, Q1707, Q1708, Q1709, Q1710, Q1711, Q1712, Q1713, Q1714, Q1715, Q1716, Q1717, Q1718, Q1719, Q1720, Q1721, Q1722, Q1723, Q1724, Q1725, Q1726, Q1727, Q1728, Q1729, Q1730, Q1731, Q1732, Q1733, Q1734, Q1735, Q1736, Q1737, Q1738, Q1739, Q1740, Q1741, Q1742, Q1743, Q1744, Q1745, Q1746, Q1747, Q1748, Q1749, Q1750, Q1751, Q1752, Q1753, Q1754, Q1755, Q1756, Q1757, Q1758, Q1759, Q1760, Q1761, Q1762, Q1763, Q1764, Q1765, Q1766, Q1767, Q1768, Q1769, Q1770, Q1771, Q1772, Q1773, Q1774, Q1775, Q1776, Q1777, Q1778, Q1779, Q1780, Q1781, Q1782, Q1783, Q1784, Q1785, Q1786, Q1787, Q1788, Q1789, Q1790, Q1791, Q1792, Q1793, Q1794, Q1795, Q1796, Q1797, Q1798, Q1799, Q1800, Q1801, Q1802, Q1803, Q1804, Q1805, Q1806, Q1807, Q1808, Q1809, Q1810, Q1811, Q1812, Q1813, Q1814, Q1815, Q1816, Q1817, Q1818, Q1819, Q1820, Q1821, Q1822, Q1823, Q1824, Q1825, Q1826, Q1827, Q1828, Q1829, Q1830, Q1831, Q1832, Q1833, Q1834, Q1835, Q1836, Q1837, Q1838, Q1839, Q1840, Q1841, Q1842, Q1843, Q1844, Q1845, Q1846, Q1847, Q1848, Q1849, Q1850, Q1851, Q1852, Q1853, Q1854, Q1855, Q1856, Q1857, Q1858, Q1859, Q1860, Q1861, Q1862, Q1863, Q1864, Q1865, Q1866, Q1867, Q1868, Q1869, Q1870, Q1871, Q1872, Q1873, Q1874, Q1875, Q1876, Q1877, Q1878, Q1879, Q1880, Q1881, Q1882, Q1883, Q1884, Q1885, Q1886, Q1887, Q1888, Q1889, Q1890, Q1891, Q1892, Q1893, Q1894, Q1895, Q1896, Q1897, Q1898, Q1899, Q1900, Q1901, Q1902, Q1903, Q1904, Q1905, Q1906, Q1907, Q1908, Q1909, Q1910, Q1911, Q1912, Q1913, Q1914, Q1915, Q1916, Q1917, Q1918, Q1919, Q1920, Q1921, Q1922, Q1923, Q1924, Q1925, Q1926, Q1927, Q1928, Q1929, Q1930, Q1931, Q1932, Q1933, Q1934, Q1935, Q1936, Q1937, Q1938, Q1939, Q1940, Q1941, Q1942, Q1943, Q1944, Q1945, Q1946, Q1947, Q1948, Q1949, Q1950, Q1951, Q1952, Q1953, Q1954, Q1955, Q1956, Q1957, Q1958, Q1959, Q1960, Q1961, Q1962, Q1963, Q1964, Q1965, Q1966, Q1967, Q1968, Q1969, Q1970, Q1971, Q1972, Q1973, Q1974, Q1975, Q1976, Q1977, Q1978, Q1979, Q1980, Q1981, Q1982, Q1983, Q1984, Q1985, Q1986, Q1987, Q1988, Q1989, Q1990, Q1991, Q1992, Q1993, Q1994, Q1995, Q1996, Q1997, Q1998, Q1999, Q2000, Q2001, Q2002, Q2003, Q2004, Q2005, Q2006, Q2007, Q2008, Q2009, Q2010, Q2011, Q2012, Q2013, Q2014, Q2015, Q2016, Q2017, Q2018, Q2019, Q2020, Q2021, Q2022, Q2023, Q2024, Q2025, Q2026, Q2027, Q2028, Q2029, Q2030, Q2031, Q2032, Q2033, Q2034, Q2035, Q2036, Q2037, Q2038, Q2039, Q2040, Q2041, Q2042, Q2043, Q2044, Q2045, Q2046, Q2047, Q2048, Q2049, Q2050, Q2051, Q2052, Q2053, Q2054, Q2055, Q2056, Q2057, Q2058, Q2059, Q2060, Q2061, Q2062, Q2063, Q2064, Q2065, Q2066, Q2067, Q2068, Q2069, Q2070, Q2071, Q2072, Q2073, Q2074, Q2075, Q2076, Q2077, Q2078, Q2079, Q2080, Q2081, Q2082, Q2083, Q2084, Q2085, Q2086, Q2087, Q2088, Q2089, Q2090, Q2091, Q2092, Q2093, Q2094, Q2095, Q2096, Q2097, Q2098, Q2099, Q2100, Q2101, Q2102, Q2103, Q2104, Q2105, Q2106, Q2107, Q2108, Q2109, Q2110, Q2111, Q2112, Q2113, Q2114, Q2115, Q2116, Q2117, Q2118, Q2119, Q2120, Q2121, Q2122, Q2123, Q2124, Q2125, Q2126, Q2127, Q2128, Q2129, Q2130, Q2131, Q2132, Q2133, Q2134, Q2135, Q2136, Q2137, Q2138, Q2139, Q2140, Q2141, Q2142, Q2143, Q2144, Q2145, Q2146, Q2147, Q2148, Q2149, Q2150, Q2151, Q2152, Q2153, Q2154, Q2155, Q2156, Q2157, Q2158, Q2159, Q2160, Q2161, Q2162, Q2163, Q2164, Q2165, Q2166, Q2167, Q2168, Q2169, Q2170, Q2171, Q2172, Q2173, Q2174, Q2175, Q2176, Q2177, Q2178, Q2179, Q2180, Q2181, Q2182, Q2183, Q2184, Q2185, Q2186, Q2187, Q2188, Q2189, Q2190, Q2191, Q2192, Q2193, Q2194, Q2195, Q2196, Q2197, Q2198, Q2199, Q2200, Q2201, Q2202, Q2203, Q2204, Q2205, Q2206, Q2207, Q2208, Q2209, Q2210, Q2211, Q2212, Q2213, Q2214, Q2215, Q2216, Q2217, Q2218, Q2219, Q2220, Q2221, Q2222, Q2223, Q2224, Q2225, Q2226, Q2227, Q2228, Q2229, Q2230, Q2231, Q2232, Q2233, Q2234, Q2235, Q2236, Q2237, Q2238, Q2239, Q2240, Q2241, Q2242, Q2243, Q2244, Q2245, Q2246, Q2247, Q2248, Q2249, Q2250, Q2251, Q2252, Q2253, Q2254, Q2255, Q2256, Q2257, Q2258, Q2259, Q2260, Q2261, Q2262, Q2263, Q2264, Q2265, Q2266, Q2267, Q2268, Q2269, Q2270, Q2271, Q2272, Q2273, Q2274, Q2275, Q2276, Q2277, Q2278, Q2279, Q2280, Q2281, Q2282, Q2283, Q2284, Q2285, Q2286, Q2287, Q2288, Q2289, Q2290, Q2291, Q2292, Q2293, Q2294, Q2295, Q2296, Q2297, Q2298, Q2299, Q2300, Q2301, Q2302, Q2303, Q2304, Q2305, Q2306, Q2307, Q2308, Q2309, Q2310, Q2311, Q2312, Q2313, Q2314, Q2315, Q2316, Q2317, Q2318, Q2319, Q2320, Q2321, Q2322, Q2323, Q2324, Q2325, Q2326, Q2327, Q2328, Q2329, Q2330, Q2331, Q2332, Q2333, Q2334, Q2335, Q2336, Q2337, Q2338, Q2339, Q2340, Q2341, Q2342, Q2343, Q2344, Q2345, Q2346, Q2347, Q2348, Q2349, Q2350, Q2351, Q2352, Q2353, Q2354, Q2355, Q2356, Q2357, Q2358, Q2359, Q2360, Q2361, Q2362, Q2363, Q2364, Q2365, Q2366, Q2367, Q2368, Q2369, Q2370, Q2371, Q2372, Q2373, Q2374, Q2375, Q2376, Q2377, Q2378, Q2379, Q2380, Q2381, Q2382, Q2383, Q2384, Q2385, Q2386, Q2387, Q2388, Q2389, Q2390, Q2391, Q2392, Q2393, Q2394, Q2395, Q2396, Q2397, Q2398, Q2399, Q2400, Q2401, Q2402, Q2403, Q2404, Q2405, Q2406, Q2407, Q2408, Q2409, Q2410, Q2411, Q2412, Q2413, Q2414, Q2415, Q2416, Q2417, Q2418, Q2419, Q2420, Q2421, Q2422, Q2423, Q2424, Q2425, Q2426, Q2427, Q2428, Q2429, Q2430, Q2431, Q2432, Q2433, Q2434, Q2435, Q2436, Q2437, Q2438, Q2439, Q2440, Q2441, Q2442, Q2443, Q2444, Q2445, Q2446, Q2447, Q2448, Q2449, Q2450, Q2451, Q2452, Q2453, Q2454, Q2455, Q2456, Q2457, Q2458, Q2459, Q2460, Q2461, Q2462, Q2463, Q2464, Q2465, Q2466, Q2467, Q2468, Q2469, Q2470, Q2471, Q2472, Q2473, Q2474, Q2475, Q2476, Q2477, Q2478, Q2479, Q2480, Q2481, Q2482, Q2483, Q2484, Q2485, Q2486, Q2487, Q2488, Q2489, Q2490, Q2491, Q2492, Q2493, Q2494, Q2495, Q2496, Q2497, Q2498, Q2499, Q2500, Q2501, Q2502, Q2503, Q2504, Q2505, Q2506, Q2507, Q2508, Q2509, Q2510, Q2511, Q2512, Q2513, Q2514, Q2515, Q2516, Q2517, Q2518, Q2519, Q2520, Q2521, Q2522, Q2523, Q2524, Q2525, Q2526, Q2527, Q2528, Q2529, Q2530, Q2531, Q2532, Q2533, Q2534, Q2535, Q2536, Q2537, Q2538, Q2539, Q2540, Q2541, Q2542, Q2543, Q2544, Q2545, Q2546, Q2547, Q2548, Q2549, Q2550, Q2551, Q2552, Q2553, Q2554, Q2555, Q2556, Q2557, Q2558, Q2559, Q2560, Q2561, Q2562, Q2563, Q2564, Q2565, Q2566, Q2567, Q2568, Q2569, Q2570, Q2571, Q2572, Q2573, Q2574, Q2575, Q2576, Q2577, Q2578, Q2579, Q2580, Q2581, Q2582, Q2583, Q2584, Q2585, Q2586, Q2587, Q2588, Q2589, Q2590, Q2591, Q2592, Q2593, Q2594, Q2595, Q2596, Q2597, Q2598, Q2599, Q2600, Q2601, Q2602, Q2603, Q2604, Q2605, Q2606, Q2607, Q2608, Q2609, Q2610, Q2611, Q2612, Q2613, Q2614, Q2615, Q2616, Q2617, Q2618, Q2619, Q2620, Q2621, Q2622, Q2623, Q2624, Q2625, Q2626, Q2627, Q2628, Q2629, Q2630, Q2631, Q2632, Q2633, Q2634, Q2635, Q2636, Q2637, Q2638, Q2639, Q2640, Q2641, Q2642, Q2643, Q2644, Q2645, Q2646, Q2647, Q2648, Q2649, Q2650, Q2651, Q2652, Q2653, Q2654, Q2655, Q2656, Q2657, Q2658, Q2659, Q2660, Q2661, Q2662, Q2663, Q2664, Q2665, Q2666, Q2667, Q2668, Q2669, Q2670, Q2671, Q2672, Q2673, Q2674, Q2675, Q2676, Q2677, Q2678, Q2679, Q2680, Q2681, Q2682, Q2683, Q2684, Q2685, Q2686, Q2687, Q2688, Q2689, Q2690, Q2691, Q2692, Q2693, Q2694, Q2695, Q2696, Q2697, Q2698, Q2699, Q2700, Q2701, Q2702, Q2703, Q2704, Q2705, Q2706, Q2707, Q2708, Q2709, Q2710, Q2711, Q2712, Q2713, Q2714, Q2715, Q2716, Q2717, Q2718, Q2719, Q2720, Q2721, Q2722, Q2723, Q2724, Q2725, Q2726, Q2727, Q2728, Q2729, Q2730, Q2731, Q2732, Q2733, Q2734, Q2735, Q2736, Q2737, Q2738, Q2739, Q2740, Q2741, Q2742, Q2743, Q2744, Q2745, Q2746, Q2747, Q2748, Q2749, Q2750, Q2751, Q2752, Q2753, Q2754, Q2755, Q2756, Q2757, Q2758, Q2759, Q2760, Q2761, Q2762, Q2763, Q2764, Q2765, Q2766, Q2767, Q2768, Q2769, Q2770, Q2771, Q2772, Q2773, Q2774, Q2775, Q2776, Q2777, Q2778, Q2779, Q2780, Q2781, Q2782, Q2783, Q2784, Q2785, Q2786, Q2787, Q2788, Q2789, Q2790, Q2791, Q2792, Q2793, Q2794, Q2795, Q2796, Q2797, Q2798, Q2799, Q2800, Q2801, Q2802, Q2803, Q2804, Q2805, Q2806, Q2807, Q2808, Q2809, Q2810, Q2811, Q2812, Q2813, Q2814, Q2815, Q2816, Q2817, Q2818, Q2819, Q2820, Q2821, Q2822, Q2823, Q2824, Q2825, Q2826, Q2827, Q2828, Q2829, Q2830, Q2831, Q2832, Q2833, Q2834, Q2835, Q2836, Q2837, Q2838, Q2839, Q2840, Q2841, Q2842, Q2843, Q2844, Q2845, Q2846, Q2847, Q2848, Q2849, Q2850, Q2851, Q2852, Q2853, Q2854, Q2855, Q2856, Q2857, Q2858, Q2859, Q2860, Q2861, Q2862, Q2863, Q2864, Q2865, Q2866, Q2867, Q2868, Q2869, Q2870, Q2871, Q2872, Q2873, Q2874, Q2875, Q2876, Q2877, Q2878, Q2879, Q2880, Q2881, Q2882, Q2883, Q2884, Q2885, Q2886, Q2887, Q2888, Q2889, Q2890, Q2891, Q2892, Q2893, Q2894, Q2895, Q2896, Q2897, Q2898, Q2899, Q2900, Q2901, Q2902, Q2903, Q2904, Q2905, Q2906, Q2907, Q2908, Q2909, Q2910, Q2911, Q2912, Q2913, Q2914, Q2915, Q2916, Q2917, Q2918, Q2919, Q2920, Q2921, Q2922, Q2923, Q2924, Q2925, Q2926, Q2927, Q2928, Q2929, Q2930, Q2931, Q2932, Q2933, Q2934, Q2935, Q2936, Q2937, Q2938, Q2939, Q2940, Q2941, Q2942, Q2943, Q2944, Q2945, Q2946, Q2947, Q2948, Q2949, Q2950, Q2951, Q2952, Q2953, Q2954, Q2955, Q2956, Q2957, Q2958, Q2959, Q2960, Q2961, Q2962, Q2963, Q2964, Q2965, Q2966, Q2967, Q2968, Q2969, Q2970, Q2971, Q2972, Q2973, Q2974, Q2975, Q2976, Q2977, Q2978, Q2979, Q2980, Q2981, Q2982, Q2983, Q2984, Q2985, Q2986, Q2987, Q2988, Q2989, Q2990, Q2991, Q2992, Q2993, Q2994, Q2995, Q2996, Q2997, Q2998, Q2999, Q3000, Q3001, Q3002, Q3003, Q3004, Q3005, Q3006, Q3007, Q3008, Q3009, Q3010, Q3011, Q3012, Q3013, Q3014, Q3015, Q3016, Q3017, Q3018, Q3019, Q3020, Q3021, Q3022, Q3023, Q3024, Q3025, Q3026, Q3027, Q3028, Q3029, Q3030, Q3031, Q3032, Q3033, Q3034, Q3035, Q3036, Q3037, Q3038, Q3039, Q3040, Q3041, Q3042, Q3043, Q3044, Q3045, Q3046, Q3047, Q3048, Q3049, Q3050, Q3051, Q3052, Q3053, Q3054, Q3055, Q3056, Q3057, Q3058, Q3059, Q3060, Q3061, Q3062, Q3063, Q3064, Q3065, Q3066, Q3067, Q3068, Q3069, Q3070, Q3071]), "transformType" : TransformType.TRANSLATION_3D, "dx" : 0 * mm, "dy" : 2.24 * mm, "dz" : 0 * mm, "makeCopy" : true});
        }
        {
            var Q0;
            Q0=makeQuery(id+"F1.opRevolve","SWEPT_BODY",BODY,{"disambiguationData":[OSD([sQuery(id+"F0.wireOp",EDGE,"E1")])]});
            transform(context, id + "F15", {"entities" : qUnion([Q0]), "transformType" : TransformType.TRANSLATION_3D, "dx" : 0 * mm, "dy" : 0 * mm, "dz" : 0 * mm, "makeCopy" : true});
        }
    });
